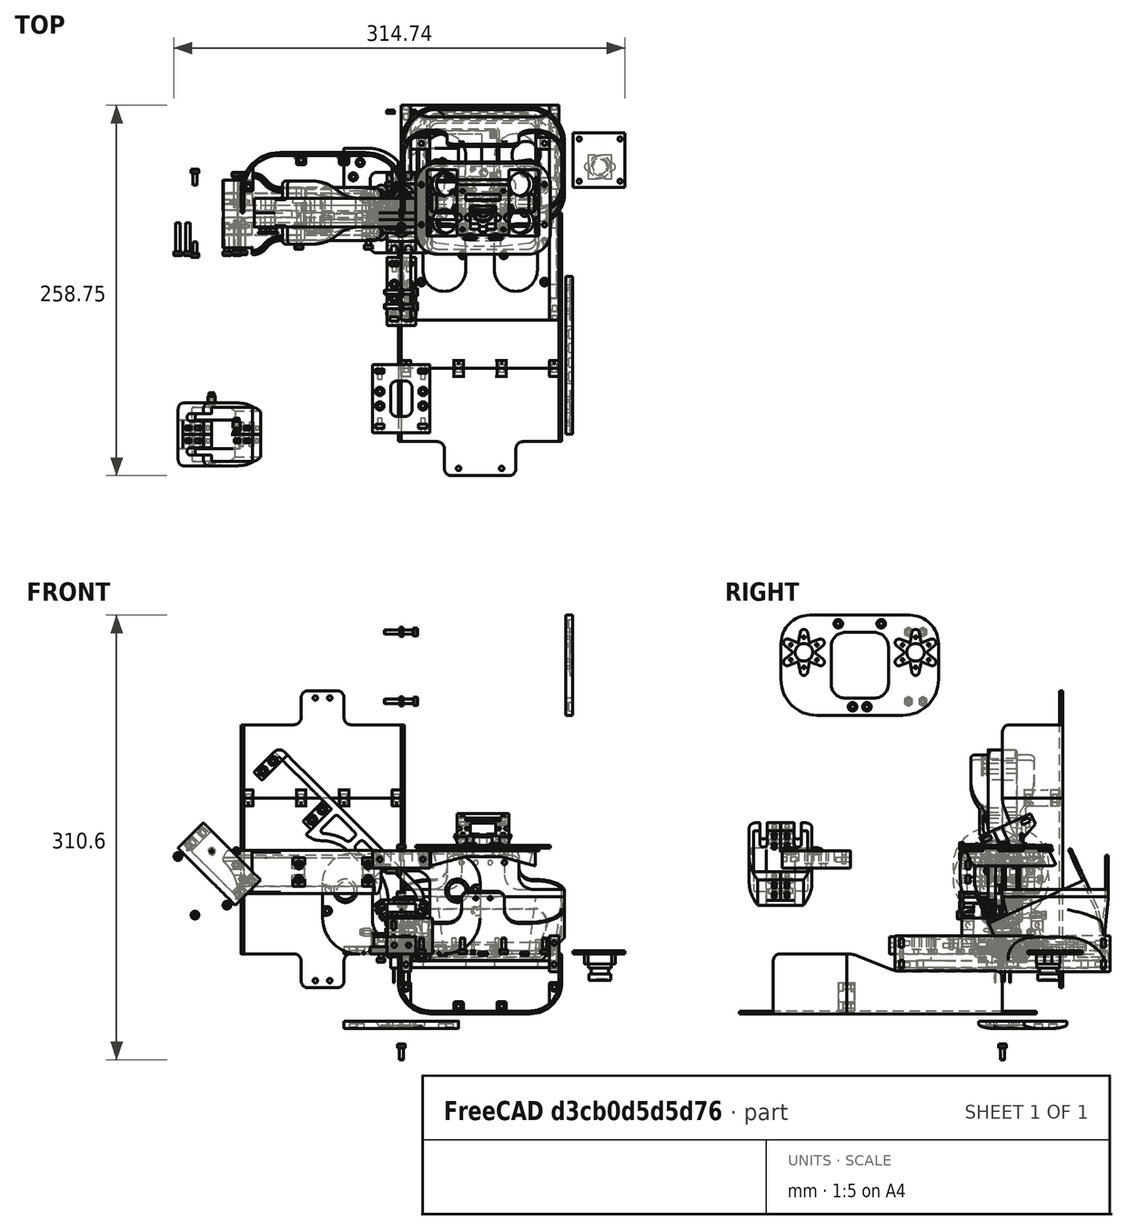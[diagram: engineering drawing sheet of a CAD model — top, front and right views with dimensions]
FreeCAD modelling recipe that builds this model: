
FCSTD DOCUMENT  (FreeCAD 0.18R4 (GitTag))
Label: spotmicroesp32_assembled_quick_and_dirty
License: CreativeCommons Attribution-NonCommercial
LicenseURL: http://creativecommons.org/licenses/by-nc/4.0/
objects: Sketcher::SketchObject×2327, PartDesign::Pad×1069, PartDesign::Pocket×818, PartDesign::Body×716, PartDesign::Chamfer×539, App::Part×291, PartDesign::Fillet×244, PartDesign::Groove×237, PartDesign::Revolution×56, PartDesign::SubtractivePipe×20, Part::Mirroring×14, Part::FeaturePython×8, PartDesign::Thickness×6, PartDesign::PolarPattern×4, PartDesign::Plane×3, PartDesign::AdditiveLoft×1
note: 8263 computed .brp shape members not serialized (recipe doc carries the construction recipe); baked Part::Feature solids carry a one-line shape summary decoded from their .brp

FEATURE [Sketcher::SketchObject] Sketch241
  MapMode = 5
  Support = -> [XY_Plane067]
  sketch-geometry (9):
    g0: ArcOfCircle CenterX=0 CenterY=0 CenterZ=0 NormalX=0 NormalY=0 NormalZ=1 AngleXU=0 Radius=16.5 StartAngle=2.61799 EndAngle=5.75959
    g1: LineSegment StartX=-14.2894 StartY=8.25 StartZ=0 EndX=-1.3577 EndY=30.6484 EndZ=0
    g2: ArcOfCircle CenterX=23.5 CenterY=16.2968 CenterZ=0 NormalX=0 NormalY=0 NormalZ=1 AngleXU=0 Radius=28.7032 StartAngle=1.5708 EndAngle=2.61799
    g3: LineSegment StartX=23.5 StartY=45 StartZ=0 EndX=40 EndY=45 EndZ=0
    g4: LineSegment StartX=40 StartY=45 StartZ=0 EndX=40 EndY=15 EndZ=0
    g5: LineSegment StartX=40 StartY=15 StartZ=0 EndX=28.6962 EndY=15 EndZ=0
    g6: ArcOfCircle CenterX=28.6962 CenterY=13.2968 CenterZ=0 NormalX=0 NormalY=0 NormalZ=1 AngleXU=0 Radius=1.70319 StartAngle=1.5708 EndAngle=2.61799
    g7: LineSegment StartX=27.2211 StartY=14.1484 StartZ=0 EndX=14.2894 EndY=-8.25 EndZ=0
    g8: LineSegment [constr] StartX=-1.3577 StartY=30.6484 StartZ=0 EndX=27.2211 EndY=14.1484 EndZ=0
  constraints (21):
    c: Tangent(g0,g1) = 1.5708
    c: Tangent(g1,g2) = 1.5708
    c: Tangent(g2,g3) = 1.5708
    c: Perpendicular(g3,g4) = 4.71239
    c: Coincident(g4,g5)
    c: Horizontal(g5)
    c: Tangent(g5,g6) = -1.5708
    c: Tangent(g6,g7) = -1.5708
    c: Parallel(g7,g1)
    c: Radius(g0) = 16.5
    c: Horizontal(g3)
    c: DistanceY(g4,g4) = 30
    c: Tangent(g7,g0) = 1.5708
    c: DistanceX(g0,g4) = 40
    c: Coincident(g8,g1)
    c: Coincident(g8,g6)
    c: Perpendicular(g1,g8)
    c: DistanceX(g3,g3) = 16.5
    c: DistanceY(g0,g4) = 15
    c: Angle(g8) = -0.523599
    c: Coincident(g0,g-1)
FEATURE [PartDesign::Pad] Pad074  label="Baseplate001"
  Length = 5
  Length2 = 100
  Profile = -> Sketch241
  Type = 0
FEATURE [Sketcher::SketchObject] Sketch236
  MapMode = 5
  Placement = pos=(40,-9.6e-15,0) rot=(0.57735,0.57735,0.57735;2.0944rad)
  Support = -> [Pad074]
  sketch-geometry (4):
    g0: ArcOfCircle CenterX=35 CenterY=-21 CenterZ=0 NormalX=0 NormalY=0 NormalZ=1 AngleXU=0 Radius=26 StartAngle=1.17601 EndAngle=1.5708
    g1: LineSegment StartX=35 StartY=5 StartZ=0 EndX=35 EndY=6 EndZ=0
    g2: LineSegment StartX=35 StartY=6 StartZ=0 EndX=45 EndY=6 EndZ=0
    g3: LineSegment StartX=45 StartY=6 StartZ=0 EndX=45 EndY=3 EndZ=0
  constraints (13):
    c: Coincident(g1,g0)
    c: Vertical(g1)
    c: Horizontal(g2)
    c: Coincident(g3,g2)
    c: Vertical(g3)
    c: Coincident(g0,g3)
    c: Coincident(g1,g2)
    c: DistanceY(g1,g1) = 1
    c: DistanceY(g3,g3) = 3
    c: DistanceX(g2,g2) = 10
    c: DistanceY(g-1,g0) = 5
    c: DistanceX(g-1,g0) = 45
    c: Perpendicular(g0,g1)
FEATURE [PartDesign::SubtractivePipe] SubtractivePipe001  label="Smooth Surfaces001"
  AuxilleryCurvelinear = true
  AuxillerySpineTangent = false
  BaseFeature = -> Pad074
  Binormal = (0,0,0)
  Mode = 0
  Profile = -> Sketch236
  Spine = -> Pad074 [Edge19,Edge22,Edge24,Edge4,Edge7,Edge10,Edge13]
  SpineTangent = false
  Transformation = 0
  Transition = 0
FEATURE [Sketcher::SketchObject] Sketch243
  MapMode = 5
  Placement = pos=(0,0,5) rot=(0,0,1;0rad)
  Support = -> [SubtractivePipe001]
  sketch-geometry (3):
    g0: Circle [constr] CenterX=0 CenterY=15 CenterZ=0 NormalX=0 NormalY=0 NormalZ=1 AngleXU=0 Radius=35
    g1: Circle CenterX=28.7228 CenterY=35 CenterZ=0 NormalX=0 NormalY=0 NormalZ=1 AngleXU=0 Radius=2.85
    g2: Circle CenterX=33.541 CenterY=25 CenterZ=0 NormalX=0 NormalY=0 NormalZ=1 AngleXU=0 Radius=2.85
  constraints (9):
    c: PointOnObject(g1,g0)
    c: PointOnObject(g2,g0)
    c: Radius(g0) = 35
    c: Equal(g2,g1)
    c: Radius(g1) = 2.85
    c: DistanceY(g2,g1) = 10
    c: DistanceY(g-1,g0) = 15
    c: DistanceY(g0,g2) = 10
    c: DistanceX(g-1,g0) = 0
FEATURE [PartDesign::Fillet] Fillet043  label="Smooth Edges001"
  Base = -> SubtractivePipe001 [Edge21]
  BaseFeature = -> SubtractivePipe001
  Radius = 1.5
FEATURE [PartDesign::Pocket] Pocket125  label="Screwheads Montage001"
  BaseFeature = -> Fillet043
  Length = 3
  Length2 = 100
  Profile = -> Sketch243
  Type = 0
FEATURE [Sketcher::SketchObject] Sketch234
  MapMode = 5
  Placement = pos=(0,0,2) rot=(0,0,1;0rad)
  Support = -> [Pocket125]
  sketch-geometry (3):
    g0: Circle [constr] CenterX=0 CenterY=15 CenterZ=0 NormalX=0 NormalY=0 NormalZ=1 AngleXU=0 Radius=35
    g1: Circle CenterX=28.7228 CenterY=35 CenterZ=0 NormalX=0 NormalY=0 NormalZ=1 AngleXU=0 Radius=1.6
    g2: Circle CenterX=33.541 CenterY=25 CenterZ=0 NormalX=0 NormalY=0 NormalZ=1 AngleXU=0 Radius=1.6
  constraints (9):
    c: Radius(g0) = 35
    c: PointOnObject(g1,g0)
    c: PointOnObject(g2,g0)
    c: Equal(g2,g1)
    c: Radius(g2) = 1.6
    c: DistanceY(g2,g1) = 10
    c: DistanceY(g-1,g0) = 15
    c: DistanceY(g0,g2) = 10
    c: DistanceX(g-1,g0) = 0
FEATURE [PartDesign::Pocket] Pocket124  label="Screwholes Montage001"
  BaseFeature = -> Pocket125
  Length = 3
  Length2 = 100
  Profile = -> Sketch234
  Type = 0
FEATURE [Sketcher::SketchObject] Sketch235
  MapMode = 5
  Placement = pos=(0,0,5) rot=(0,0,1;0rad)
  Support = -> [Fillet043]
  sketch-geometry (33):
    g0: LineSegment [constr] StartX=11.6913 StartY=6.75 StartZ=0 EndX=0 EndY=13.5 EndZ=0
    g1: LineSegment [constr] StartX=0 StartY=13.5 StartZ=0 EndX=-11.6913 EndY=6.75 EndZ=0
    g2: LineSegment [constr] StartX=-11.6913 StartY=6.75 StartZ=0 EndX=-11.6913 EndY=-6.75 EndZ=0
    g3: LineSegment [constr] StartX=-11.6913 StartY=-6.75 StartZ=0 EndX=0 EndY=-13.5 EndZ=0
    g4: LineSegment [constr] StartX=-6e-16 StartY=-13.5 StartZ=0 EndX=11.6913 EndY=-6.75 EndZ=0
    g5: LineSegment [constr] StartX=11.6913 StartY=-6.75 StartZ=0 EndX=11.6913 EndY=6.75 EndZ=0
    g6: Circle [constr] CenterX=0 CenterY=0 CenterZ=0 NormalX=0 NormalY=0 NormalZ=1 AngleXU=0 Radius=13.5
    g7: LineSegment [constr] StartX=7.5 StartY=9e-16 StartZ=0 EndX=3.75 EndY=6.49519 EndZ=0
    g8: LineSegment [constr] StartX=3.75 StartY=6.49519 StartZ=0 EndX=-3.75 EndY=6.49519 EndZ=0
    g9: LineSegment [constr] StartX=-3.75 StartY=6.49519 StartZ=0 EndX=-7.5 EndY=-9e-16 EndZ=0
    g10: LineSegment [constr] StartX=-7.5 StartY=-9e-16 StartZ=0 EndX=-3.75 EndY=-6.49519 EndZ=0
    g11: LineSegment [constr] StartX=-3.75 StartY=-6.49519 StartZ=0 EndX=3.75 EndY=-6.49519 EndZ=0
    g12: LineSegment [constr] StartX=3.75 StartY=-6.49519 StartZ=0 EndX=7.5 EndY=9e-16 EndZ=0
    g13: Circle [constr] CenterX=0 CenterY=0 CenterZ=0 NormalX=0 NormalY=0 NormalZ=1 AngleXU=0 Radius=7.5
    g14: ArcOfCircle CenterX=11.6913 CenterY=-6.75 CenterZ=0 NormalX=0 NormalY=0 NormalZ=1 AngleXU=0 Radius=2.6 StartAngle=4.34694 EndAngle=7.17223
    g15: ArcOfCircle CenterX=-6e-16 CenterY=-13.5 CenterZ=0 NormalX=0 NormalY=0 NormalZ=1 AngleXU=0 Radius=2.6 StartAngle=3.29974 EndAngle=6.12503
    g16: ArcOfCircle CenterX=-11.6913 CenterY=-6.75 CenterZ=0 NormalX=0 NormalY=0 NormalZ=1 AngleXU=0 Radius=2.6 StartAngle=2.25255 EndAngle=5.07784
    g17: ArcOfCircle CenterX=-11.6913 CenterY=6.75 CenterZ=0 NormalX=0 NormalY=0 NormalZ=1 AngleXU=0 Radius=2.6 StartAngle=1.20535 EndAngle=4.03064
    g18: ArcOfCircle CenterX=0 CenterY=13.5 CenterZ=0 NormalX=0 NormalY=0 NormalZ=1 AngleXU=0 Radius=2.6 StartAngle=0.15815 EndAngle=2.98344
    g19: ArcOfCircle CenterX=11.6913 CenterY=6.75 CenterZ=0 NormalX=0 NormalY=0 NormalZ=1 AngleXU=0 Radius=2.6 StartAngle=5.39414 EndAngle=8.21943
    g20: LineSegment StartX=13.3297 StartY=4.73117 StartZ=0 EndX=7.5 EndY=9e-16 EndZ=0
    g21: LineSegment StartX=7.5 StartY=9e-16 StartZ=0 EndX=13.3297 EndY=-4.73117 EndZ=0
    g22: LineSegment StartX=10.7622 StartY=-9.17831 StartZ=0 EndX=3.75 EndY=-6.49519 EndZ=0
    g23: LineSegment StartX=3.75 StartY=-6.49519 StartZ=0 EndX=2.56755 EndY=-13.9095 EndZ=0
    g24: LineSegment StartX=-2.56755 StartY=-13.9095 StartZ=0 EndX=-3.75 EndY=-6.49519 EndZ=0
    g25: LineSegment StartX=-3.75 StartY=-6.49519 StartZ=0 EndX=-10.7622 EndY=-9.17831 EndZ=0
    g26: LineSegment StartX=-13.3297 StartY=-4.73117 StartZ=0 EndX=-7.5 EndY=-9e-16 EndZ=0
    g27: LineSegment StartX=-7.5 StartY=-9e-16 StartZ=0 EndX=-13.3297 EndY=4.73117 EndZ=0
    g28: LineSegment StartX=-10.7622 StartY=9.17831 StartZ=0 EndX=-3.75 EndY=6.49519 EndZ=0
    g29: LineSegment StartX=-3.75 StartY=6.49519 StartZ=0 EndX=-2.56755 EndY=13.9095 EndZ=0
    g30: LineSegment StartX=2.56755 StartY=13.9095 StartZ=0 EndX=3.75 EndY=6.49519 EndZ=0
    g31: LineSegment StartX=3.75 StartY=6.49519 StartZ=0 EndX=10.7622 EndY=9.17831 EndZ=0
    g32: LineSegment [constr] StartX=11.6913 StartY=6.75 StartZ=0 EndX=-11.6913 EndY=-6.75 EndZ=0
  constraints (70):
    c: Coincident(g0,g1)
    c: Coincident(g1,g2)
    c: Coincident(g2,g3)
    c: Coincident(g3,g4)
    c: Coincident(g4,g5)
    c: Coincident(g5,g0)
    c: Equal(g0, g1-g5) x5
    c: PointOnObject(g0,g6)
    c: PointOnObject(g1,g6)
    c: PointOnObject(g2,g6)
    c: PointOnObject(g3,g6)
    c: PointOnObject(g4,g6)
    c: PointOnObject(g5,g6)
    c: Coincident(g6,g-1)
    c: Radius(g6) = 13.5
    c: Coincident(g7,g8)
    c: Coincident(g8,g9)
    c: Coincident(g9,g10)
    c: Coincident(g10,g11)
    c: Coincident(g11,g12)
    c: Coincident(g12,g7)
    c: Equal(g7, g8-g12) x5
    c: PointOnObject(g7,g13)
    c: PointOnObject(g8,g13)
    c: PointOnObject(g9,g13)
    c: PointOnObject(g10,g13)
    c: PointOnObject(g11,g13)
    c: PointOnObject(g12,g13)
    c: Coincident(g13,g-1)
    c: Radius(g13) = 7.5
    c: Coincident(g14,g4)
    c: Coincident(g15,g3)
    c: Coincident(g16,g2)
    c: Coincident(g17,g1)
    c: Coincident(g18,g0)
    c: Coincident(g19,g0)
    c: Coincident(g20,g7)
    c: Coincident(g21,g20)
    c: Coincident(g22,g11)
    c: Coincident(g23,g22)
    c: Coincident(g24,g10)
    c: Coincident(g25,g24)
    c: Coincident(g26,g9)
    c: Coincident(g28,g8)
    c: Coincident(g29,g28)
    c: Coincident(g30,g7)
    c: Coincident(g31,g30)
    c: Tangent(g22,g14) = 1.5708
    c: Tangent(g23,g15) = 1.5708
    c: Tangent(g24,g15) = 1.5708
    c: Tangent(g26,g16) = 1.5708
    c: Tangent(g21,g14) = 1.5708
    c: Tangent(g16,g25) = 1.5708
    c: Tangent(g29,g18) = 1.5708
    c: Tangent(g30,g18) = 1.5708
    c: Tangent(g31,g19) = 1.5708
    c: Tangent(g20,g19) = 1.5708
    c: Tangent(g27,g17) = 1.5708
    c: Tangent(g17,g28) = 1.5708
    c: Coincident(g27,g26)
    c: Equal(g14,g15)
    c: Equal(g15,g16)
    c: Equal(g16,g17)
    c: Equal(g17,g18)
    c: Equal(g18,g19)
    c: Radius(g14) = 2.6
    c: Coincident(g32,g19)
    c: Coincident(g32,g16)
    c: Perpendicular(g32,g7)
    c: PointOnObject(g18,g-2)
FEATURE [PartDesign::Pocket] Pocket123  label="Servohorn003"
  BaseFeature = -> Pocket124
  Length = 2
  Length2 = 100
  Profile = -> Sketch235
  Type = 0
FEATURE [PartDesign::Fillet] Fillet041  label="Smooth Servhohorn Edges001"
  Base = -> Pocket123 [Edge124,Edge122,Edge129,Edge121,Edge136,Edge120]
  BaseFeature = -> Pocket123
  Radius = 1
FEATURE [Sketcher::SketchObject] Sketch242
  MapMode = 5
  Placement = pos=(0,0,3) rot=(0,0,1;0rad)
  Support = -> [Fillet041]
  sketch-geometry (14):
    g0: LineSegment [constr] StartX=0 StartY=10.5 StartZ=0 EndX=-9.09327 EndY=5.25 EndZ=0
    g1: LineSegment [constr] StartX=-9.09327 StartY=5.25 StartZ=0 EndX=-9.09327 EndY=-5.25 EndZ=0
    g2: LineSegment [constr] StartX=-9.09327 StartY=-5.25 StartZ=0 EndX=0 EndY=-10.5 EndZ=0
    g3: LineSegment [constr] StartX=0 StartY=-10.5 StartZ=0 EndX=9.09327 EndY=-5.25 EndZ=0
    g4: LineSegment [constr] StartX=9.09327 StartY=-5.25 StartZ=0 EndX=9.09327 EndY=5.25 EndZ=0
    g5: LineSegment [constr] StartX=9.09327 StartY=5.25 StartZ=0 EndX=0 EndY=10.5 EndZ=0
    g6: Circle [constr] CenterX=0 CenterY=0 CenterZ=0 NormalX=0 NormalY=0 NormalZ=1 AngleXU=0 Radius=10.5
    g7: LineSegment [constr] StartX=0 StartY=10.5 StartZ=0 EndX=0 EndY=-10.5 EndZ=0
    g8: Circle CenterX=0 CenterY=10.5 CenterZ=0 NormalX=0 NormalY=0 NormalZ=1 AngleXU=0 Radius=0.95
    g9: Circle CenterX=9.09327 CenterY=5.25 CenterZ=0 NormalX=0 NormalY=0 NormalZ=1 AngleXU=0 Radius=0.95
    g10: Circle CenterX=9.09327 CenterY=-5.25 CenterZ=0 NormalX=0 NormalY=0 NormalZ=1 AngleXU=0 Radius=0.95
    g11: Circle CenterX=0 CenterY=-10.5 CenterZ=0 NormalX=0 NormalY=0 NormalZ=1 AngleXU=0 Radius=0.95
    g12: Circle CenterX=-9.09327 CenterY=-5.25 CenterZ=0 NormalX=0 NormalY=0 NormalZ=1 AngleXU=0 Radius=0.95
    g13: Circle CenterX=-9.09327 CenterY=5.25 CenterZ=0 NormalX=0 NormalY=0 NormalZ=1 AngleXU=0 Radius=0.95
  constraints (30):
    c: Coincident(g0,g1)
    c: Coincident(g1,g2)
    c: Coincident(g2,g3)
    c: Coincident(g3,g4)
    c: Coincident(g4,g5)
    c: Coincident(g5,g0)
    c: Equal(g0, g1-g5) x5
    c: PointOnObject(g0,g6)
    c: PointOnObject(g1,g6)
    c: PointOnObject(g2,g6)
    c: PointOnObject(g3,g6)
    c: PointOnObject(g4,g6)
    c: PointOnObject(g5,g6)
    c: Coincident(g6,g-1)
    c: Coincident(g7,g0)
    c: Coincident(g7,g2)
    c: Radius(g6) = 10.5
    c: Coincident(g8,g0)
    c: Coincident(g9,g4)
    c: Coincident(g10,g3)
    c: Coincident(g11,g2)
    c: Coincident(g12,g1)
    c: Coincident(g13,g0)
    c: Equal(g13,g12)
    c: Equal(g12,g11)
    c: Equal(g11,g10)
    c: Equal(g10,g9)
    c: Equal(g9,g8)
    c: Radius(g8) = 0.95
    c: PointOnObject(g8,g-2)
FEATURE [PartDesign::Pocket] Pocket126  label="Servohorn Mounting Holes001"
  BaseFeature = -> Fillet041
  Length = 3
  Length2 = 100
  Profile = -> Sketch242
  Type = 0
FEATURE [Sketcher::SketchObject] Sketch239
  MapMode = 5
  Placement = pos=(0,0,3) rot=(0,0,1;0rad)
  Support = -> [Pocket126]
  sketch-geometry (1):
    g0: Circle CenterX=0 CenterY=0 CenterZ=0 NormalX=0 NormalY=0 NormalZ=1 AngleXU=0 Radius=6.15
  constraints (2):
    c: Coincident(g0,g-1)
    c: Radius(g0) = 6.15
FEATURE [PartDesign::Pocket] Pocket122  label="Servohorn Axis001"
  BaseFeature = -> Pocket126
  Length = 3
  Length2 = 100
  Profile = -> Sketch239
  Type = 0
FEATURE [PartDesign::Fillet] Fillet042  label="Smooth End Egde001"
  Base = -> Pocket122 [Edge150]
  BaseFeature = -> Pocket122
  Radius = 0.4
FEATURE [PartDesign::Body] Body041  label="Limb_Servohorn_Mount_long_v005"
  Group = -> [Sketch241,Pad074,Sketch236,SubtractivePipe001,Fillet043,Sketch243,Pocket125,Sketch234,Pocket124,Sketch235,Pocket123,Fillet041,Sketch242,Pocket126,Sketch239,Pocket122,Fillet042]
  Origin = -> Origin071
  Tip = -> Fillet042
FEATURE [Sketcher::SketchObject] Sketch244
  MapMode = 5
  Support = -> [XY_Plane063]
  sketch-geometry (64):
    g0: LineSegment [constr] StartX=-3.75 StartY=6.49519 StartZ=0 EndX=-7.5 EndY=0 EndZ=0
    g1: LineSegment [constr] StartX=-7.5 StartY=0 StartZ=0 EndX=-3.75 EndY=-6.49519 EndZ=0
    g2: LineSegment [constr] StartX=-3.75 StartY=-6.49519 StartZ=0 EndX=3.75 EndY=-6.49519 EndZ=0
    g3: LineSegment [constr] StartX=3.75 StartY=-6.49519 StartZ=0 EndX=7.5 EndY=0 EndZ=0
    g4: LineSegment [constr] StartX=7.5 StartY=0 StartZ=0 EndX=3.75 EndY=6.49519 EndZ=0
    g5: LineSegment [constr] StartX=3.75 StartY=6.49519 StartZ=0 EndX=-3.75 EndY=6.49519 EndZ=0
    g6: Circle [constr] CenterX=0 CenterY=0 CenterZ=0 NormalX=0 NormalY=0 NormalZ=1 AngleXU=0 Radius=7.5
    g7: LineSegment [constr] StartX=0 StartY=7.5 StartZ=0 EndX=-6.49519 EndY=3.75 EndZ=0
    g8: LineSegment [constr] StartX=-6.49519 StartY=3.75 StartZ=0 EndX=-6.49519 EndY=-3.75 EndZ=0
    g9: LineSegment [constr] StartX=-6.49519 StartY=-3.75 StartZ=0 EndX=9.8e-15 EndY=-7.5 EndZ=0
    g10: LineSegment [constr] StartX=9.8e-15 StartY=-7.5 StartZ=0 EndX=6.49519 EndY=-3.75 EndZ=0
    g11: LineSegment [constr] StartX=6.49519 StartY=-3.75 StartZ=0 EndX=6.49519 EndY=3.75 EndZ=0
    g12: LineSegment [constr] StartX=6.49519 StartY=3.75 StartZ=0 EndX=0 EndY=7.5 EndZ=0
    g13: Circle [constr] CenterX=0 CenterY=0 CenterZ=0 NormalX=0 NormalY=0 NormalZ=1 AngleXU=0 Radius=7.5
    g14: LineSegment [constr] StartX=0 StartY=10.5 StartZ=0 EndX=-9.09327 EndY=5.25 EndZ=0
    g15: LineSegment [constr] StartX=-9.09327 StartY=5.25 StartZ=0 EndX=-9.09327 EndY=-5.25 EndZ=0
    g16: LineSegment [constr] StartX=-9.09327 StartY=-5.25 StartZ=0 EndX=-1.42e-14 EndY=-10.5 EndZ=0
    g17: LineSegment [constr] StartX=-1.42e-14 StartY=-10.5 StartZ=0 EndX=9.09327 EndY=-5.25 EndZ=0
    g18: LineSegment [constr] StartX=9.09327 StartY=-5.25 StartZ=0 EndX=9.09327 EndY=5.25 EndZ=0
    g19: LineSegment [constr] StartX=9.09327 StartY=5.25 StartZ=0 EndX=0 EndY=10.5 EndZ=0
    g20: Circle [constr] CenterX=0 CenterY=0 CenterZ=0 NormalX=0 NormalY=0 NormalZ=1 AngleXU=0 Radius=10.5
    g21: LineSegment [constr] StartX=0 StartY=13.5 StartZ=0 EndX=-11.6913 EndY=6.75 EndZ=0
    g22: LineSegment [constr] StartX=-11.6913 StartY=6.75 StartZ=0 EndX=-11.6913 EndY=-6.75 EndZ=0
    g23: LineSegment [constr] StartX=-11.6913 StartY=-6.75 StartZ=0 EndX=0 EndY=-13.5 EndZ=0
    g24: LineSegment [constr] StartX=0 StartY=-13.5 StartZ=0 EndX=11.6913 EndY=-6.75 EndZ=0
    g25: LineSegment [constr] StartX=11.6913 StartY=-6.75 StartZ=0 EndX=11.6913 EndY=6.75 EndZ=0
    g26: LineSegment [constr] StartX=11.6913 StartY=6.75 StartZ=0 EndX=0 EndY=13.5 EndZ=0
    g27: Circle [constr] CenterX=0 CenterY=0 CenterZ=0 NormalX=0 NormalY=0 NormalZ=1 AngleXU=0 Radius=13.5
    g28: ArcOfCircle CenterX=0 CenterY=13.5 CenterZ=0 NormalX=0 NormalY=0 NormalZ=1 AngleXU=0 Radius=2.5 StartAngle=0.171439 EndAngle=2.97015
    g29: ArcOfCircle CenterX=11.6913 CenterY=6.75 CenterZ=0 NormalX=0 NormalY=0 NormalZ=1 AngleXU=0 Radius=2.5 StartAngle=5.40743 EndAngle=8.20614
    g30: ArcOfCircle CenterX=11.6913 CenterY=-6.75 CenterZ=0 NormalX=0 NormalY=0 NormalZ=1 AngleXU=0 Radius=2.5 StartAngle=4.36023 EndAngle=7.15894
    g31: ArcOfCircle CenterX=0 CenterY=-13.5 CenterZ=0 NormalX=0 NormalY=0 NormalZ=1 AngleXU=0 Radius=2.5 StartAngle=3.31303 EndAngle=6.11175
    g32: ArcOfCircle CenterX=-11.6913 CenterY=-6.75 CenterZ=0 NormalX=0 NormalY=0 NormalZ=1 AngleXU=0 Radius=2.5 StartAngle=2.26583 EndAngle=5.06455
    g33: ArcOfCircle CenterX=-11.6913 CenterY=6.75 CenterZ=0 NormalX=0 NormalY=0 NormalZ=1 AngleXU=0 Radius=2.5 StartAngle=1.21864 EndAngle=4.01735
    g34: LineSegment StartX=-10.829 StartY=9.09658 StartZ=0 EndX=-3.75 EndY=6.49519 EndZ=0
    g35: LineSegment StartX=-3.75 StartY=6.49519 StartZ=0 EndX=-2.46335 EndY=13.9265 EndZ=0
    g36: LineSegment StartX=2.46335 StartY=13.9265 StartZ=0 EndX=3.75 EndY=6.49519 EndZ=0
    g37: LineSegment StartX=3.75 StartY=6.49519 StartZ=0 EndX=10.829 EndY=9.09658 EndZ=0
    g38: LineSegment StartX=13.2924 StartY=4.82993 StartZ=0 EndX=7.5 EndY=0 EndZ=0
    g39: LineSegment StartX=7.5 StartY=0 StartZ=0 EndX=13.2924 EndY=-4.82993 EndZ=0
    g40: LineSegment StartX=10.829 StartY=-9.09658 StartZ=0 EndX=3.75 EndY=-6.49519 EndZ=0
    g41: LineSegment StartX=3.75 StartY=-6.49519 StartZ=0 EndX=2.46335 EndY=-13.9265 EndZ=0
    g42: LineSegment StartX=-2.46335 StartY=-13.9265 StartZ=0 EndX=-3.75 EndY=-6.49519 EndZ=0
    g43: LineSegment StartX=-3.75 StartY=-6.49519 StartZ=0 EndX=-10.829 EndY=-9.09658 EndZ=0
    g44: LineSegment StartX=-13.2924 StartY=-4.82993 StartZ=0 EndX=-7.5 EndY=0 EndZ=0
    g45: LineSegment StartX=-7.5 StartY=0 StartZ=0 EndX=-13.2924 EndY=4.82993 EndZ=0
    g46: Circle CenterX=-11.6913 CenterY=6.75 CenterZ=0 NormalX=0 NormalY=0 NormalZ=1 AngleXU=0 Radius=0.75
    g47: Circle CenterX=-9.09327 CenterY=5.25 CenterZ=0 NormalX=0 NormalY=0 NormalZ=1 AngleXU=0 Radius=0.75
    g48: Circle CenterX=-6.49519 CenterY=3.75 CenterZ=0 NormalX=0 NormalY=0 NormalZ=1 AngleXU=0 Radius=0.75
    g49: Circle CenterX=0 CenterY=13.5 CenterZ=0 NormalX=0 NormalY=0 NormalZ=1 AngleXU=0 Radius=0.75
    g50: Circle CenterX=0 CenterY=10.5 CenterZ=0 NormalX=0 NormalY=0 NormalZ=1 AngleXU=0 Radius=0.75
    g51: Circle CenterX=0 CenterY=7.5 CenterZ=0 NormalX=0 NormalY=0 NormalZ=1 AngleXU=0 Radius=0.75
    g52: Circle CenterX=11.6913 CenterY=6.75 CenterZ=0 NormalX=0 NormalY=0 NormalZ=1 AngleXU=0 Radius=0.75
    g53: Circle CenterX=9.09327 CenterY=5.25 CenterZ=0 NormalX=0 NormalY=0 NormalZ=1 AngleXU=0 Radius=0.75
    g54: Circle CenterX=6.49519 CenterY=3.75 CenterZ=0 NormalX=0 NormalY=0 NormalZ=1 AngleXU=0 Radius=0.75
    g55: Circle CenterX=11.6913 CenterY=-6.75 CenterZ=0 NormalX=0 NormalY=0 NormalZ=1 AngleXU=0 Radius=0.75
    g56: Circle CenterX=9.09327 CenterY=-5.25 CenterZ=0 NormalX=0 NormalY=0 NormalZ=1 AngleXU=0 Radius=0.75
    g57: Circle CenterX=6.49519 CenterY=-3.75 CenterZ=0 NormalX=0 NormalY=0 NormalZ=1 AngleXU=0 Radius=0.75
    g58: Circle CenterX=9.8e-15 CenterY=-7.5 CenterZ=0 NormalX=0 NormalY=0 NormalZ=1 AngleXU=0 Radius=0.75
    g59: Circle CenterX=-1.42e-14 CenterY=-10.5 CenterZ=0 NormalX=0 NormalY=0 NormalZ=1 AngleXU=0 Radius=0.75
    g60: Circle CenterX=0 CenterY=-13.5 CenterZ=0 NormalX=0 NormalY=0 NormalZ=1 AngleXU=0 Radius=0.75
    g61: Circle CenterX=-11.6913 CenterY=-6.75 CenterZ=0 NormalX=0 NormalY=0 NormalZ=1 AngleXU=0 Radius=0.75
    g62: Circle CenterX=-9.09327 CenterY=-5.25 CenterZ=0 NormalX=0 NormalY=0 NormalZ=1 AngleXU=0 Radius=0.75
    g63: Circle CenterX=-6.49519 CenterY=-3.75 CenterZ=0 NormalX=0 NormalY=0 NormalZ=1 AngleXU=0 Radius=0.75
  constraints (136):
    c: Coincident(g0,g1)
    c: Coincident(g1,g2)
    c: Coincident(g2,g3)
    c: Coincident(g3,g4)
    c: Coincident(g4,g5)
    c: Coincident(g5,g0)
    c: Equal(g0, g1-g5) x5
    c: PointOnObject(g0,g6)
    c: PointOnObject(g1,g6)
    c: PointOnObject(g2,g6)
    c: PointOnObject(g3,g6)
    c: PointOnObject(g4,g6)
    c: PointOnObject(g5,g6)
    c: Coincident(g6,g-1)
    c: Coincident(g7,g8)
    c: Coincident(g8,g9)
    c: Coincident(g9,g10)
    c: Coincident(g10,g11)
    c: Coincident(g11,g12)
    c: Coincident(g12,g7)
    c: Equal(g7, g8-g12) x5
    c: PointOnObject(g7,g13)
    c: PointOnObject(g8,g13)
    c: PointOnObject(g9,g13)
    c: PointOnObject(g10,g13)
    c: PointOnObject(g11,g13)
    c: PointOnObject(g12,g13)
    c: Coincident(g13,g-1)
    c: PointOnObject(g12,g6)
    c: PointOnObject(g7,g-2)
    c: Horizontal(g5)
    c: Radius(g6) = 7.5
    c: Coincident(g14,g15)
    c: Coincident(g15,g16)
    c: Coincident(g16,g17)
    c: Coincident(g17,g18)
    c: Coincident(g18,g19)
    c: Coincident(g19,g14)
    c: Equal(g14, g15-g19) x5
    c: PointOnObject(g14,g20)
    c: PointOnObject(g15,g20)
    c: PointOnObject(g16,g20)
    c: PointOnObject(g17,g20)
    c: PointOnObject(g18,g20)
    c: PointOnObject(g19,g20)
    c: Coincident(g20,g-1)
    c: PointOnObject(g19,g-2)
    c: Radius(g20) = 10.5
    c: Coincident(g21,g22)
    c: Coincident(g22,g23)
    c: Coincident(g23,g24)
    c: Coincident(g24,g25)
    c: Coincident(g25,g26)
    c: Coincident(g26,g21)
    c: Equal(g21, g22-g26) x5
    c: PointOnObject(g21,g27)
    c: PointOnObject(g22,g27)
    c: PointOnObject(g23,g27)
    c: PointOnObject(g24,g27)
    c: PointOnObject(g25,g27)
    c: PointOnObject(g26,g27)
    c: Coincident(g27,g-1)
    c: PointOnObject(g26,g-2)
    c: Radius(g27) = 13.5
    c: Coincident(g28,g21)
    c: Coincident(g29,g25)
    c: Coincident(g30,g24)
    c: Coincident(g31,g23)
    c: Coincident(g32,g22)
    c: Coincident(g33,g21)
    c: Coincident(g34,g0)
    c: Coincident(g35,g34)
    c: Coincident(g36,g4)
    c: Coincident(g37,g36)
    c: Coincident(g38,g3)
    c: Coincident(g39,g38)
    c: Coincident(g40,g2)
    c: Coincident(g41,g40)
    c: Coincident(g42,g1)
    c: Coincident(g43,g42)
    c: Coincident(g44,g0)
    c: Coincident(g45,g44)
    c: Tangent(g35,g28) = 1.5708
    c: Tangent(g36,g28) = 1.5708
    c: Tangent(g37,g29) = 1.5708
    c: Tangent(g38,g29) = 1.5708
    c: Tangent(g39,g30) = 1.5708
    c: Tangent(g40,g30) = 1.5708
    c: Tangent(g41,g31) = 1.5708
    c: Tangent(g42,g31) = 1.5708
    c: Tangent(g43,g32) = 1.5708
    c: Tangent(g44,g32) = 1.5708
    c: Tangent(g45,g33) = 1.5708
    c: Tangent(g34,g33) = 1.5708
    c: Radius(g29) = 2.5
    c: Equal(g29,g28)
    c: Equal(g28,g33)
    c: Equal(g33,g32)
    c: Equal(g32,g31)
    c: Equal(g31,g30)
    c: Coincident(g46,g33)
    c: Coincident(g47,g14)
    c: Coincident(g48,g7)
    c: Coincident(g49,g28)
    c: Coincident(g50,g14)
    c: Coincident(g51,g7)
    c: Coincident(g52,g29)
    c: Coincident(g53,g18)
    c: Coincident(g54,g11)
    c: Coincident(g55,g30)
    c: Coincident(g56,g17)
    c: Coincident(g57,g10)
    c: Coincident(g58,g9)
    c: Coincident(g59,g16)
    c: Coincident(g60,g31)
    c: Coincident(g61,g32)
    c: Coincident(g62,g15)
    c: Coincident(g63,g8)
    c: Equal(g61,g62)
    c: Equal(g62,g63)
    c: Equal(g63,g58)
    c: Equal(g58,g59)
    c: Equal(g59,g60)
    c: Equal(g60,g55)
    c: Equal(g55,g56)
    c: Equal(g56,g57)
    c: Equal(g57,g54)
    c: Equal(g54,g53)
    c: Equal(g53,g52)
    c: Equal(g52,g51)
    c: Equal(g51,g50)
    c: Equal(g50,g49)
    c: Equal(g49,g46)
    c: Equal(g46,g47)
    c: Equal(g47,g48)
    c: Radius(g55) = 0.75
FEATURE [PartDesign::Pad] Pad075
  Length = 2
  Length2 = 100
  Profile = -> Sketch244
  Type = 0
FEATURE [Sketcher::SketchObject] Sketch237
  MapMode = 5
  Placement = pos=(0,0,2) rot=(0,0,1;0rad)
  Support = -> [Pad075]
  sketch-geometry (2):
    g0: Circle CenterX=0 CenterY=0 CenterZ=0 NormalX=0 NormalY=0 NormalZ=1 AngleXU=0 Radius=5
    g1: Circle CenterX=0 CenterY=0 CenterZ=0 NormalX=0 NormalY=0 NormalZ=1 AngleXU=0 Radius=3.5
  constraints (4):
    c: Coincident(g0,g-1)
    c: Coincident(g1,g0)
    c: Radius(g1) = 3.5
    c: Radius(g0) = 5
FEATURE [PartDesign::Pocket] Pocket121
  BaseFeature = -> Pad075
  Length = 1
  Length2 = 100
  Profile = -> Sketch237
  Type = 0
FEATURE [Sketcher::SketchObject] Sketch238
  MapMode = 5
  Placement = pos=(0,0,2) rot=(0,0,1;0rad)
  Support = -> [Pocket121]
  sketch-geometry (1):
    g0: Circle CenterX=0 CenterY=0 CenterZ=0 NormalX=0 NormalY=0 NormalZ=1 AngleXU=0 Radius=3
  constraints (2):
    c: Coincident(g0,g-1)
    c: Radius(g0) = 3
FEATURE [PartDesign::Pocket] Pocket127
  BaseFeature = -> Pocket121
  Length = 1
  Length2 = 100
  Profile = -> Sketch238
  Type = 0
FEATURE [Sketcher::SketchObject] Sketch240
  MapMode = 5
  Placement = pos=(0,0,1) rot=(0,0,1;0rad)
  Support = -> [Pocket127]
  sketch-geometry (1):
    g0: Circle CenterX=0 CenterY=0 CenterZ=0 NormalX=0 NormalY=0 NormalZ=1 AngleXU=0 Radius=1.5
  constraints (2):
    c: Coincident(g0,g-1)
    c: Radius(g0) = 1.5
FEATURE [PartDesign::Pocket] Pocket130
  BaseFeature = -> Pocket127
  Length = 5
  Length2 = 100
  Profile = -> Sketch240
  Type = 0
FEATURE [Sketcher::SketchObject] Sketch245
  MapMode = 5
  Placement = pos=(0,0,0) rot=(1,0,0;3.14159rad)
  Support = -> [Pocket130]
  sketch-geometry (2):
    g0: Circle CenterX=0 CenterY=0 CenterZ=0 NormalX=0 NormalY=0 NormalZ=1 AngleXU=0 Radius=4.5
    g1: Circle CenterX=0 CenterY=0 CenterZ=0 NormalX=0 NormalY=0 NormalZ=1 AngleXU=0 Radius=3
  constraints (4):
    c: Coincident(g0,g-1)
    c: Coincident(g1,g0)
    c: Radius(g0) = 4.5
    c: Radius(g1) = 3
FEATURE [PartDesign::Pad] Pad073
  BaseFeature = -> Pocket130
  Length = 3
  Length2 = 100
  Profile = -> Sketch245
  Type = 0
FEATURE [PartDesign::Fillet] Fillet044
  Base = -> Pad073 [Face5,Edge96,Face4]
  BaseFeature = -> Pad073
  Radius = 0.2
FEATURE [PartDesign::Body] Body042  label="Futuba FSH6B001"
  Group = -> [Sketch244,Pad075,Sketch237,Pocket121,Sketch238,Pocket127,Sketch240,Pocket130,Sketch245,Pad073,Fillet044]
  Origin = -> Origin075
  Tip = -> Fillet044
FEATURE [App::Part] Part013  label="Servohorn002"
  Group = -> [Body042]
  Origin = -> Origin072
  Placement = pos=(0,0,3) rot=(0,0,1;0rad)
FEATURE [Sketcher::SketchObject] Sketch247
  MapMode = 5
  Support = -> [XY_Plane079]
FEATURE [Sketcher::SketchObject] Sketch249
  MapMode = 5
  Support = -> [XY_Plane078]
  sketch-geometry (1):
    g0: Circle CenterX=0 CenterY=0 CenterZ=0 NormalX=0 NormalY=0 NormalZ=1 AngleXU=0 Radius=1.9
  constraints (2):
    c: Coincident(g0,g-1)
    c: Radius(g0) = 1.9
FEATURE [PartDesign::Pad] Pad078  label="M3x8 Head007"
  Length = 2
  Length2 = 100
  Profile = -> Sketch249
  Type = 0
FEATURE [Sketcher::SketchObject] Sketch250
  MapMode = 5
  Placement = pos=(0,0,2) rot=(0,0,1;0rad)
  Support = -> [Pad078]
  sketch-geometry (1):
    g0: Circle CenterX=0 CenterY=0 CenterZ=0 NormalX=0 NormalY=0 NormalZ=1 AngleXU=0 Radius=1
  constraints (2):
    c: Coincident(g0,g-1)
    c: Radius(g0) = 1
FEATURE [PartDesign::Pad] Pad079  label="M3x8 Thread007"
  BaseFeature = -> Pad078
  Length = 8
  Length2 = 100
  Profile = -> Sketch250
  Type = 0
FEATURE [Sketcher::SketchObject] Sketch246
  MapMode = 5
  Placement = pos=(0,0,0) rot=(1,0,0;3.14159rad)
  Support = -> [Pad079]
  sketch-geometry (7):
    g0: LineSegment StartX=0.77 StartY=0.44456 StartZ=0 EndX=0 EndY=0.889119 EndZ=0
    g1: LineSegment StartX=0 StartY=0.889119 StartZ=0 EndX=-0.77 EndY=0.44456 EndZ=0
    g2: LineSegment StartX=-0.77 StartY=0.44456 StartZ=0 EndX=-0.77 EndY=-0.44456 EndZ=0
    g3: LineSegment StartX=-0.77 StartY=-0.44456 StartZ=0 EndX=3.85628e-11 EndY=-0.889119 EndZ=0
    g4: LineSegment StartX=3.85628e-11 StartY=-0.889119 StartZ=0 EndX=0.77 EndY=-0.44456 EndZ=0
    g5: LineSegment StartX=0.77 StartY=-0.44456 StartZ=0 EndX=0.77 EndY=0.44456 EndZ=0
    g6: Circle [constr] CenterX=0 CenterY=0 CenterZ=0 NormalX=0 NormalY=0 NormalZ=1 AngleXU=0 Radius=0.889119
  constraints (16):
    c: Coincident(g0,g1)
    c: Coincident(g1,g2)
    c: Coincident(g2,g3)
    c: Coincident(g3,g4)
    c: Coincident(g4,g5)
    c: Coincident(g5,g0)
    c: Equal(g0, g1-g5) x5
    c: PointOnObject(g0,g6)
    c: PointOnObject(g1,g6)
    c: PointOnObject(g2,g6)
    c: PointOnObject(g3,g6)
    c: PointOnObject(g4,g6)
    c: PointOnObject(g5,g6)
    c: Coincident(g6,g-1)
    c: PointOnObject(g0,g-2)
    c: DistanceX(g1,g0) = 1.54
FEATURE [PartDesign::Pocket] Pocket129  label="M3x8 Wrench008"
  BaseFeature = -> Pad079
  Length = 1
  Length2 = 100
  Profile = -> Sketch246
  Type = 0
FEATURE [PartDesign::Chamfer] Chamfer025  label="M3x8 Smooth012"
  Base = -> Pocket129 [Face11,Edge2,Edge24,Edge3]
  BaseFeature = -> Pocket129
  Size = 0.2
FEATURE [Sketcher::SketchObject] Sketch251
  MapMode = 5
  Support = -> [XY_Plane079]
FEATURE [Sketcher::SketchObject] Sketch252
  MapMode = 5
  Support = -> [XY_Plane079]
  sketch-geometry (8):
    g0: LineSegment StartX=0 StartY=2.3094 StartZ=0 EndX=-2 EndY=1.1547 EndZ=0
    g1: LineSegment StartX=-2 StartY=1.1547 StartZ=0 EndX=-2 EndY=-1.1547 EndZ=0
    g2: LineSegment StartX=-2 StartY=-1.1547 StartZ=0 EndX=-2e-16 EndY=-2.3094 EndZ=0
    g3: LineSegment StartX=-2e-16 StartY=-2.3094 StartZ=0 EndX=2 EndY=-1.1547 EndZ=0
    g4: LineSegment StartX=2 StartY=-1.1547 StartZ=0 EndX=2 EndY=1.1547 EndZ=0
    g5: LineSegment StartX=2 StartY=1.1547 StartZ=0 EndX=0 EndY=2.3094 EndZ=0
    g6: Circle [constr] CenterX=0 CenterY=0 CenterZ=0 NormalX=0 NormalY=0 NormalZ=1 AngleXU=0 Radius=2.3094
    g7: Circle CenterX=0 CenterY=0 CenterZ=0 NormalX=0 NormalY=0 NormalZ=1 AngleXU=0 Radius=1
  constraints (18):
    c: Coincident(g0,g1)
    c: Coincident(g1,g2)
    c: Coincident(g2,g3)
    c: Coincident(g3,g4)
    c: Coincident(g4,g5)
    c: Coincident(g5,g0)
    c: Equal(g0, g1-g5) x5
    c: PointOnObject(g0,g6)
    c: PointOnObject(g1,g6)
    c: PointOnObject(g2,g6)
    c: PointOnObject(g3,g6)
    c: PointOnObject(g4,g6)
    c: PointOnObject(g5,g6)
    c: Coincident(g6,g-1)
    c: PointOnObject(g5,g-2)
    c: DistanceX(g0,g4) = 4
    c: Coincident(g7,g-1)
    c: Radius(g7) = 1
FEATURE [PartDesign::Pad] Pad077  label="M3 Nut Primitive008"
  Length = 0.6
  Length2 = 0.6
  Profile = -> Sketch252
  Type = 4
FEATURE [Sketcher::SketchObject] Sketch248
  ExternalGeometry = -> [Pad077]
  MapMode = 5
  Placement = pos=(0,0,0) rot=(0.57735,0.57735,0.57735;2.0944rad)
  Support = -> [YZ_Plane078]
  sketch-geometry (6):
    g0: LineSegment StartX=-1.9594 StartY=0.6 StartZ=0 EndX=-2.8094 EndY=0.6 EndZ=0
    g1: LineSegment StartX=-2.8094 StartY=0.6 StartZ=0 EndX=-2.8094 EndY=-0.6 EndZ=0
    g2: LineSegment StartX=-2.8094 StartY=-0.6 StartZ=0 EndX=-1.9594 EndY=-0.6 EndZ=0
    g3: LineSegment StartX=-1.9594 StartY=-0.6 StartZ=0 EndX=-2.3094 EndY=-0.4 EndZ=0
    g4: LineSegment StartX=-2.3094 StartY=-0.4 StartZ=0 EndX=-2.3094 EndY=0.4 EndZ=0
    g5: LineSegment StartX=-2.3094 StartY=0.4 StartZ=0 EndX=-1.9594 EndY=0.6 EndZ=0
  constraints (15):
    c: Horizontal(g0)
    c: Coincident(g0,g1)
    c: Coincident(g1,g2)
    c: Coincident(g2,g3)
    c: Coincident(g3,g4)
    c: Coincident(g4,g5)
    c: Coincident(g5,g0)
    c: Symmetric(g4,g3,g-1)
    c: Symmetric(g0,g2,g-1)
    c: Symmetric(g1,g0,g-1)
    c: DistanceX(g0,g4) = 0.5
    c: DistanceY(g3,g4) = 0.8
    c: DistanceY(g1,g0) = 1.2
    c: PointOnObject(g3,g-3)
    c: DistanceX(g4,g0) = 0.35
FEATURE [PartDesign::Groove] Groove007  label="M3 Nut Smooth007"
  Angle = 360
  Axis = (-2e-16,3e-16,1)
  Base = (0,0,0)
  BaseFeature = -> Pad077
  Profile = -> Sketch248
  ReferenceAxis = -> Sketch248 [V_Axis]
  Reversed = true
FEATURE [PartDesign::Chamfer] Chamfer022  label="M3 Nut Smooth Hole010"
  Base = -> Groove007 [Edge24,Edge23]
  BaseFeature = -> Groove007
  Size = 0.2
FEATURE [Sketcher::SketchObject] Sketch253
  MapMode = 5
  Support = -> [XY_Plane058]
FEATURE [Sketcher::SketchObject] Sketch256
  MapMode = 5
  Support = -> [XY_Plane060]
  sketch-geometry (8):
    g0: LineSegment StartX=0 StartY=2.3094 StartZ=0 EndX=-2 EndY=1.1547 EndZ=0
    g1: LineSegment StartX=-2 StartY=1.1547 StartZ=0 EndX=-2 EndY=-1.1547 EndZ=0
    g2: LineSegment StartX=-2 StartY=-1.1547 StartZ=0 EndX=-2e-16 EndY=-2.3094 EndZ=0
    g3: LineSegment StartX=-2e-16 StartY=-2.3094 StartZ=0 EndX=2 EndY=-1.1547 EndZ=0
    g4: LineSegment StartX=2 StartY=-1.1547 StartZ=0 EndX=2 EndY=1.1547 EndZ=0
    g5: LineSegment StartX=2 StartY=1.1547 StartZ=0 EndX=0 EndY=2.3094 EndZ=0
    g6: Circle [constr] CenterX=0 CenterY=0 CenterZ=0 NormalX=0 NormalY=0 NormalZ=1 AngleXU=0 Radius=2.3094
    g7: Circle CenterX=0 CenterY=0 CenterZ=0 NormalX=0 NormalY=0 NormalZ=1 AngleXU=0 Radius=1
  constraints (18):
    c: Coincident(g0,g1)
    c: Coincident(g1,g2)
    c: Coincident(g2,g3)
    c: Coincident(g3,g4)
    c: Coincident(g4,g5)
    c: Coincident(g5,g0)
    c: Equal(g0, g1-g5) x5
    c: PointOnObject(g0,g6)
    c: PointOnObject(g1,g6)
    c: PointOnObject(g2,g6)
    c: PointOnObject(g3,g6)
    c: PointOnObject(g4,g6)
    c: PointOnObject(g5,g6)
    c: Coincident(g6,g-1)
    c: PointOnObject(g5,g-2)
    c: DistanceX(g0,g4) = 4
    c: Coincident(g7,g-1)
    c: Radius(g7) = 1
FEATURE [PartDesign::Pad] Pad086  label="M3 Nut Primitive010"
  Length = 0.6
  Length2 = 0.6
  Profile = -> Sketch256
  Type = 4
FEATURE [Sketcher::SketchObject] Sketch254
  ExternalGeometry = -> [Pad086]
  MapMode = 5
  Placement = pos=(0,0,0) rot=(0.57735,0.57735,0.57735;2.0944rad)
  Support = -> [YZ_Plane058]
  sketch-geometry (6):
    g0: LineSegment StartX=-1.9594 StartY=0.6 StartZ=0 EndX=-2.8094 EndY=0.6 EndZ=0
    g1: LineSegment StartX=-2.8094 StartY=0.6 StartZ=0 EndX=-2.8094 EndY=-0.6 EndZ=0
    g2: LineSegment StartX=-2.8094 StartY=-0.6 StartZ=0 EndX=-1.9594 EndY=-0.6 EndZ=0
    g3: LineSegment StartX=-1.9594 StartY=-0.6 StartZ=0 EndX=-2.3094 EndY=-0.4 EndZ=0
    g4: LineSegment StartX=-2.3094 StartY=-0.4 StartZ=0 EndX=-2.3094 EndY=0.4 EndZ=0
    g5: LineSegment StartX=-2.3094 StartY=0.4 StartZ=0 EndX=-1.9594 EndY=0.6 EndZ=0
  constraints (15):
    c: Horizontal(g0)
    c: Coincident(g0,g1)
    c: Coincident(g1,g2)
    c: Coincident(g2,g3)
    c: Coincident(g3,g4)
    c: Coincident(g4,g5)
    c: Coincident(g5,g0)
    c: Symmetric(g4,g3,g-1)
    c: Symmetric(g0,g2,g-1)
    c: Symmetric(g1,g0,g-1)
    c: DistanceX(g0,g4) = 0.5
    c: DistanceY(g3,g4) = 0.8
    c: DistanceY(g1,g0) = 1.2
    c: PointOnObject(g3,g-3)
    c: DistanceX(g4,g0) = 0.35
FEATURE [PartDesign::Groove] Groove009  label="M3 Nut Smooth009"
  Angle = 360
  Axis = (-2e-16,3e-16,1)
  Base = (0,0,0)
  BaseFeature = -> Pad086
  Profile = -> Sketch254
  ReferenceAxis = -> Sketch254 [V_Axis]
  Reversed = true
FEATURE [PartDesign::Chamfer] Chamfer019  label="M3 Nut Smooth Hole009"
  Base = -> Groove009 [Edge24,Edge23]
  BaseFeature = -> Groove009
  Size = 0.2
FEATURE [Sketcher::SketchObject] Sketch257
  MapMode = 5
  Support = -> [XY_Plane075]
  sketch-geometry (8):
    g0: LineSegment StartX=0 StartY=2.3094 StartZ=0 EndX=-2 EndY=1.1547 EndZ=0
    g1: LineSegment StartX=-2 StartY=1.1547 StartZ=0 EndX=-2 EndY=-1.1547 EndZ=0
    g2: LineSegment StartX=-2 StartY=-1.1547 StartZ=0 EndX=-2e-16 EndY=-2.3094 EndZ=0
    g3: LineSegment StartX=-2e-16 StartY=-2.3094 StartZ=0 EndX=2 EndY=-1.1547 EndZ=0
    g4: LineSegment StartX=2 StartY=-1.1547 StartZ=0 EndX=2 EndY=1.1547 EndZ=0
    g5: LineSegment StartX=2 StartY=1.1547 StartZ=0 EndX=0 EndY=2.3094 EndZ=0
    g6: Circle [constr] CenterX=0 CenterY=0 CenterZ=0 NormalX=0 NormalY=0 NormalZ=1 AngleXU=0 Radius=2.3094
    g7: Circle CenterX=0 CenterY=0 CenterZ=0 NormalX=0 NormalY=0 NormalZ=1 AngleXU=0 Radius=1
  constraints (18):
    c: Coincident(g0,g1)
    c: Coincident(g1,g2)
    c: Coincident(g2,g3)
    c: Coincident(g3,g4)
    c: Coincident(g4,g5)
    c: Coincident(g5,g0)
    c: Equal(g0, g1-g5) x5
    c: PointOnObject(g0,g6)
    c: PointOnObject(g1,g6)
    c: PointOnObject(g2,g6)
    c: PointOnObject(g3,g6)
    c: PointOnObject(g4,g6)
    c: PointOnObject(g5,g6)
    c: Coincident(g6,g-1)
    c: PointOnObject(g5,g-2)
    c: DistanceX(g0,g4) = 4
    c: Coincident(g7,g-1)
    c: Radius(g7) = 1
FEATURE [PartDesign::Pad] Pad084  label="M3 Nut Primitive009"
  Length = 0.6
  Length2 = 0.6
  Profile = -> Sketch257
  Type = 4
FEATURE [Sketcher::SketchObject] Sketch258
  MapMode = 5
  Support = -> [XY_Plane061]
  sketch-geometry (1):
    g0: Circle CenterX=0 CenterY=0 CenterZ=0 NormalX=0 NormalY=0 NormalZ=1 AngleXU=0 Radius=1.9
  constraints (2):
    c: Coincident(g0,g-1)
    c: Radius(g0) = 1.9
FEATURE [PartDesign::Pad] Pad082  label="M3x8 Head009"
  Length = 2
  Length2 = 100
  Profile = -> Sketch258
  Type = 0
FEATURE [Sketcher::SketchObject] Sketch259
  MapMode = 5
  Support = -> [XY_Plane060]
FEATURE [Sketcher::SketchObject] Sketch260
  MapMode = 5
  Support = -> [XY_Plane058]
FEATURE [Sketcher::SketchObject] Sketch261
  MapMode = 5
  Support = -> [XY_Plane060]
FEATURE [PartDesign::Body] Body037  label="M2 Nut006"
  Group = -> [Sketch256,Pad086,Sketch254,Groove009,Chamfer019,Sketch261,Sketch259]
  Origin = -> Origin060
  Placement = pos=(0,0,2.75) rot=(0,0,1;0rad)
  Tip = -> Chamfer019
FEATURE [Sketcher::SketchObject] Sketch262
  MapMode = 5
  Support = -> [XY_Plane076]
  sketch-geometry (1):
    g0: Circle CenterX=0 CenterY=0 CenterZ=0 NormalX=0 NormalY=0 NormalZ=1 AngleXU=0 Radius=1.9
  constraints (2):
    c: Coincident(g0,g-1)
    c: Radius(g0) = 1.9
FEATURE [PartDesign::Pad] Pad080  label="M3x8 Head008"
  Length = 2
  Length2 = 100
  Profile = -> Sketch262
  Type = 0
FEATURE [Sketcher::SketchObject] Sketch263
  MapMode = 5
  Placement = pos=(0,0,2) rot=(0,0,1;0rad)
  Support = -> [Pad082]
  sketch-geometry (1):
    g0: Circle CenterX=0 CenterY=0 CenterZ=0 NormalX=0 NormalY=0 NormalZ=1 AngleXU=0 Radius=1
  constraints (2):
    c: Coincident(g0,g-1)
    c: Radius(g0) = 1
FEATURE [PartDesign::Pad] Pad085  label="M3x8 Thread010"
  BaseFeature = -> Pad082
  Length = 8
  Length2 = 100
  Profile = -> Sketch263
  Type = 0
FEATURE [Sketcher::SketchObject] Sketch264
  MapMode = 5
  Placement = pos=(0,0,0) rot=(1,0,0;3.14159rad)
  Support = -> [Pad085]
  sketch-geometry (7):
    g0: LineSegment StartX=0.77 StartY=0.44456 StartZ=0 EndX=0 EndY=0.889119 EndZ=0
    g1: LineSegment StartX=0 StartY=0.889119 StartZ=0 EndX=-0.77 EndY=0.44456 EndZ=0
    g2: LineSegment StartX=-0.77 StartY=0.44456 StartZ=0 EndX=-0.77 EndY=-0.44456 EndZ=0
    g3: LineSegment StartX=-0.77 StartY=-0.44456 StartZ=0 EndX=3.85628e-11 EndY=-0.889119 EndZ=0
    g4: LineSegment StartX=3.85628e-11 StartY=-0.889119 StartZ=0 EndX=0.77 EndY=-0.44456 EndZ=0
    g5: LineSegment StartX=0.77 StartY=-0.44456 StartZ=0 EndX=0.77 EndY=0.44456 EndZ=0
    g6: Circle [constr] CenterX=0 CenterY=0 CenterZ=0 NormalX=0 NormalY=0 NormalZ=1 AngleXU=0 Radius=0.889119
  constraints (16):
    c: Coincident(g0,g1)
    c: Coincident(g1,g2)
    c: Coincident(g2,g3)
    c: Coincident(g3,g4)
    c: Coincident(g4,g5)
    c: Coincident(g5,g0)
    c: Equal(g0, g1-g5) x5
    c: PointOnObject(g0,g6)
    c: PointOnObject(g1,g6)
    c: PointOnObject(g2,g6)
    c: PointOnObject(g3,g6)
    c: PointOnObject(g4,g6)
    c: PointOnObject(g5,g6)
    c: Coincident(g6,g-1)
    c: PointOnObject(g0,g-2)
    c: DistanceX(g1,g0) = 1.54
FEATURE [PartDesign::Pocket] Pocket131  label="M3x8 Wrench009"
  BaseFeature = -> Pad085
  Length = 1
  Length2 = 100
  Profile = -> Sketch264
  Type = 0
FEATURE [PartDesign::Chamfer] Chamfer024  label="M3x8 Smooth011"
  Base = -> Pocket131 [Face11,Edge2,Edge24,Edge3]
  BaseFeature = -> Pocket131
  Size = 0.2
FEATURE [Sketcher::SketchObject] Sketch265
  MapMode = 5
  Support = -> [XY_Plane058]
  sketch-geometry (8):
    g0: LineSegment StartX=0 StartY=2.3094 StartZ=0 EndX=-2 EndY=1.1547 EndZ=0
    g1: LineSegment StartX=-2 StartY=1.1547 StartZ=0 EndX=-2 EndY=-1.1547 EndZ=0
    g2: LineSegment StartX=-2 StartY=-1.1547 StartZ=0 EndX=-2e-16 EndY=-2.3094 EndZ=0
    g3: LineSegment StartX=-2e-16 StartY=-2.3094 StartZ=0 EndX=2 EndY=-1.1547 EndZ=0
    g4: LineSegment StartX=2 StartY=-1.1547 StartZ=0 EndX=2 EndY=1.1547 EndZ=0
    g5: LineSegment StartX=2 StartY=1.1547 StartZ=0 EndX=0 EndY=2.3094 EndZ=0
    g6: Circle [constr] CenterX=0 CenterY=0 CenterZ=0 NormalX=0 NormalY=0 NormalZ=1 AngleXU=0 Radius=2.3094
    g7: Circle CenterX=0 CenterY=0 CenterZ=0 NormalX=0 NormalY=0 NormalZ=1 AngleXU=0 Radius=1
  constraints (18):
    c: Coincident(g0,g1)
    c: Coincident(g1,g2)
    c: Coincident(g2,g3)
    c: Coincident(g3,g4)
    c: Coincident(g4,g5)
    c: Coincident(g5,g0)
    c: Equal(g0, g1-g5) x5
    c: PointOnObject(g0,g6)
    c: PointOnObject(g1,g6)
    c: PointOnObject(g2,g6)
    c: PointOnObject(g3,g6)
    c: PointOnObject(g4,g6)
    c: PointOnObject(g5,g6)
    c: Coincident(g6,g-1)
    c: PointOnObject(g5,g-2)
    c: DistanceX(g0,g4) = 4
    c: Coincident(g7,g-1)
    c: Radius(g7) = 1
FEATURE [PartDesign::Pad] Pad076  label="M3 Nut Primitive007"
  Length = 0.6
  Length2 = 0.6
  Profile = -> Sketch265
  Type = 4
FEATURE [Sketcher::SketchObject] Sketch255
  ExternalGeometry = -> [Pad076]
  MapMode = 5
  Placement = pos=(0,0,0) rot=(0.57735,0.57735,0.57735;2.0944rad)
  Support = -> [YZ_Plane057]
  sketch-geometry (6):
    g0: LineSegment StartX=-1.9594 StartY=0.6 StartZ=0 EndX=-2.8094 EndY=0.6 EndZ=0
    g1: LineSegment StartX=-2.8094 StartY=0.6 StartZ=0 EndX=-2.8094 EndY=-0.6 EndZ=0
    g2: LineSegment StartX=-2.8094 StartY=-0.6 StartZ=0 EndX=-1.9594 EndY=-0.6 EndZ=0
    g3: LineSegment StartX=-1.9594 StartY=-0.6 StartZ=0 EndX=-2.3094 EndY=-0.4 EndZ=0
    g4: LineSegment StartX=-2.3094 StartY=-0.4 StartZ=0 EndX=-2.3094 EndY=0.4 EndZ=0
    g5: LineSegment StartX=-2.3094 StartY=0.4 StartZ=0 EndX=-1.9594 EndY=0.6 EndZ=0
  constraints (15):
    c: Horizontal(g0)
    c: Coincident(g0,g1)
    c: Coincident(g1,g2)
    c: Coincident(g2,g3)
    c: Coincident(g3,g4)
    c: Coincident(g4,g5)
    c: Coincident(g5,g0)
    c: Symmetric(g4,g3,g-1)
    c: Symmetric(g0,g2,g-1)
    c: Symmetric(g1,g0,g-1)
    c: DistanceX(g0,g4) = 0.5
    c: DistanceY(g3,g4) = 0.8
    c: DistanceY(g1,g0) = 1.2
    c: PointOnObject(g3,g-3)
    c: DistanceX(g4,g0) = 0.35
FEATURE [PartDesign::Groove] Groove008  label="M3 Nut Smooth008"
  Angle = 360
  Axis = (-2e-16,3e-16,1)
  Base = (0,0,0)
  BaseFeature = -> Pad076
  Profile = -> Sketch255
  ReferenceAxis = -> Sketch255 [V_Axis]
  Reversed = true
FEATURE [PartDesign::Chamfer] Chamfer023  label="M3 Nut Smooth Hole011"
  Base = -> Groove008 [Edge24,Edge23]
  BaseFeature = -> Groove008
  Size = 0.2
FEATURE [Sketcher::SketchObject] Sketch267
  MapMode = 5
  Placement = pos=(0,0,2) rot=(0,0,1;0rad)
  Support = -> [Pad080]
  sketch-geometry (1):
    g0: Circle CenterX=0 CenterY=0 CenterZ=0 NormalX=0 NormalY=0 NormalZ=1 AngleXU=0 Radius=1
  constraints (2):
    c: Coincident(g0,g-1)
    c: Radius(g0) = 1
FEATURE [PartDesign::Pad] Pad081  label="M3x8 Thread008"
  BaseFeature = -> Pad080
  Length = 8
  Length2 = 100
  Profile = -> Sketch267
  Type = 0
FEATURE [Sketcher::SketchObject] Sketch266
  MapMode = 5
  Placement = pos=(0,0,0) rot=(1,0,0;3.14159rad)
  Support = -> [Pad081]
  sketch-geometry (7):
    g0: LineSegment StartX=0.77 StartY=0.44456 StartZ=0 EndX=0 EndY=0.889119 EndZ=0
    g1: LineSegment StartX=0 StartY=0.889119 StartZ=0 EndX=-0.77 EndY=0.44456 EndZ=0
    g2: LineSegment StartX=-0.77 StartY=0.44456 StartZ=0 EndX=-0.77 EndY=-0.44456 EndZ=0
    g3: LineSegment StartX=-0.77 StartY=-0.44456 StartZ=0 EndX=3.85628e-11 EndY=-0.889119 EndZ=0
    g4: LineSegment StartX=3.85628e-11 StartY=-0.889119 StartZ=0 EndX=0.77 EndY=-0.44456 EndZ=0
    g5: LineSegment StartX=0.77 StartY=-0.44456 StartZ=0 EndX=0.77 EndY=0.44456 EndZ=0
    g6: Circle [constr] CenterX=0 CenterY=0 CenterZ=0 NormalX=0 NormalY=0 NormalZ=1 AngleXU=0 Radius=0.889119
  constraints (16):
    c: Coincident(g0,g1)
    c: Coincident(g1,g2)
    c: Coincident(g2,g3)
    c: Coincident(g3,g4)
    c: Coincident(g4,g5)
    c: Coincident(g5,g0)
    c: Equal(g0, g1-g5) x5
    c: PointOnObject(g0,g6)
    c: PointOnObject(g1,g6)
    c: PointOnObject(g2,g6)
    c: PointOnObject(g3,g6)
    c: PointOnObject(g4,g6)
    c: PointOnObject(g5,g6)
    c: Coincident(g6,g-1)
    c: PointOnObject(g0,g-2)
    c: DistanceX(g1,g0) = 1.54
FEATURE [PartDesign::Pocket] Pocket132  label="M3x8 Wrench010"
  BaseFeature = -> Pad081
  Length = 1
  Length2 = 100
  Profile = -> Sketch266
  Type = 0
FEATURE [PartDesign::Chamfer] Chamfer020  label="M3x8 Smooth009"
  Base = -> Pocket132 [Face11,Edge2,Edge24,Edge3]
  BaseFeature = -> Pocket132
  Size = 0.2
FEATURE [PartDesign::Body] Body038  label="M2x014"
  Group = -> [Sketch262,Pad080,Sketch267,Pad081,Sketch266,Pocket132,Chamfer020]
  Origin = -> Origin068
  Tip = -> Chamfer020
FEATURE [App::Part] Part016  label="M010"
  Group = -> [Body038,Body037]
  Origin = -> Origin059
  Placement = pos=(-9.1,-5.25,80) rot=(0,1,0;3.14159rad)
FEATURE [Sketcher::SketchObject] Sketch268
  ExternalGeometry = -> [Pad084]
  MapMode = 5
  Placement = pos=(0,0,0) rot=(0.57735,0.57735,0.57735;2.0944rad)
  Support = -> [YZ_Plane073]
  sketch-geometry (6):
    g0: LineSegment StartX=-1.9594 StartY=0.6 StartZ=0 EndX=-2.8094 EndY=0.6 EndZ=0
    g1: LineSegment StartX=-2.8094 StartY=0.6 StartZ=0 EndX=-2.8094 EndY=-0.6 EndZ=0
    g2: LineSegment StartX=-2.8094 StartY=-0.6 StartZ=0 EndX=-1.9594 EndY=-0.6 EndZ=0
    g3: LineSegment StartX=-1.9594 StartY=-0.6 StartZ=0 EndX=-2.3094 EndY=-0.4 EndZ=0
    g4: LineSegment StartX=-2.3094 StartY=-0.4 StartZ=0 EndX=-2.3094 EndY=0.4 EndZ=0
    g5: LineSegment StartX=-2.3094 StartY=0.4 StartZ=0 EndX=-1.9594 EndY=0.6 EndZ=0
  constraints (15):
    c: Horizontal(g0)
    c: Coincident(g0,g1)
    c: Coincident(g1,g2)
    c: Coincident(g2,g3)
    c: Coincident(g3,g4)
    c: Coincident(g4,g5)
    c: Coincident(g5,g0)
    c: Symmetric(g4,g3,g-1)
    c: Symmetric(g0,g2,g-1)
    c: Symmetric(g1,g0,g-1)
    c: DistanceX(g0,g4) = 0.5
    c: DistanceY(g3,g4) = 0.8
    c: DistanceY(g1,g0) = 1.2
    c: PointOnObject(g3,g-3)
    c: DistanceX(g4,g0) = 0.35
FEATURE [PartDesign::Groove] Groove010  label="M3 Nut Smooth010"
  Angle = 360
  Axis = (-2e-16,3e-16,1)
  Base = (0,0,0)
  BaseFeature = -> Pad084
  Profile = -> Sketch268
  ReferenceAxis = -> Sketch268 [V_Axis]
  Reversed = true
FEATURE [PartDesign::Chamfer] Chamfer026  label="M3 Nut Smooth Hole012"
  Base = -> Groove010 [Edge24,Edge23]
  BaseFeature = -> Groove010
  Size = 0.2
FEATURE [Sketcher::SketchObject] Sketch271
  MapMode = 5
  Support = -> [XY_Plane072]
  sketch-geometry (8):
    g0: LineSegment StartX=0 StartY=2.3094 StartZ=0 EndX=-2 EndY=1.1547 EndZ=0
    g1: LineSegment StartX=-2 StartY=1.1547 StartZ=0 EndX=-2 EndY=-1.1547 EndZ=0
    g2: LineSegment StartX=-2 StartY=-1.1547 StartZ=0 EndX=-2e-16 EndY=-2.3094 EndZ=0
    g3: LineSegment StartX=-2e-16 StartY=-2.3094 StartZ=0 EndX=2 EndY=-1.1547 EndZ=0
    g4: LineSegment StartX=2 StartY=-1.1547 StartZ=0 EndX=2 EndY=1.1547 EndZ=0
    g5: LineSegment StartX=2 StartY=1.1547 StartZ=0 EndX=0 EndY=2.3094 EndZ=0
    g6: Circle [constr] CenterX=0 CenterY=0 CenterZ=0 NormalX=0 NormalY=0 NormalZ=1 AngleXU=0 Radius=2.3094
    g7: Circle CenterX=0 CenterY=0 CenterZ=0 NormalX=0 NormalY=0 NormalZ=1 AngleXU=0 Radius=1
  constraints (18):
    c: Coincident(g0,g1)
    c: Coincident(g1,g2)
    c: Coincident(g2,g3)
    c: Coincident(g3,g4)
    c: Coincident(g4,g5)
    c: Coincident(g5,g0)
    c: Equal(g0, g1-g5) x5
    c: PointOnObject(g0,g6)
    c: PointOnObject(g1,g6)
    c: PointOnObject(g2,g6)
    c: PointOnObject(g3,g6)
    c: PointOnObject(g4,g6)
    c: PointOnObject(g5,g6)
    c: Coincident(g6,g-1)
    c: PointOnObject(g5,g-2)
    c: DistanceX(g0,g4) = 4
    c: Coincident(g7,g-1)
    c: Radius(g7) = 1
FEATURE [PartDesign::Pad] Pad091  label="M3 Nut Primitive011"
  Length = 0.6
  Length2 = 0.6
  Profile = -> Sketch271
  Type = 4
FEATURE [Sketcher::SketchObject] Sketch270
  ExternalGeometry = -> [Pad091]
  MapMode = 5
  Placement = pos=(0,0,0) rot=(0.57735,0.57735,0.57735;2.0944rad)
  Support = -> [YZ_Plane067]
  sketch-geometry (6):
    g0: LineSegment StartX=-1.9594 StartY=0.6 StartZ=0 EndX=-2.8094 EndY=0.6 EndZ=0
    g1: LineSegment StartX=-2.8094 StartY=0.6 StartZ=0 EndX=-2.8094 EndY=-0.6 EndZ=0
    g2: LineSegment StartX=-2.8094 StartY=-0.6 StartZ=0 EndX=-1.9594 EndY=-0.6 EndZ=0
    g3: LineSegment StartX=-1.9594 StartY=-0.6 StartZ=0 EndX=-2.3094 EndY=-0.4 EndZ=0
    g4: LineSegment StartX=-2.3094 StartY=-0.4 StartZ=0 EndX=-2.3094 EndY=0.4 EndZ=0
    g5: LineSegment StartX=-2.3094 StartY=0.4 StartZ=0 EndX=-1.9594 EndY=0.6 EndZ=0
  constraints (15):
    c: Horizontal(g0)
    c: Coincident(g0,g1)
    c: Coincident(g1,g2)
    c: Coincident(g2,g3)
    c: Coincident(g3,g4)
    c: Coincident(g4,g5)
    c: Coincident(g5,g0)
    c: Symmetric(g4,g3,g-1)
    c: Symmetric(g0,g2,g-1)
    c: Symmetric(g1,g0,g-1)
    c: DistanceX(g0,g4) = 0.5
    c: DistanceY(g3,g4) = 0.8
    c: DistanceY(g1,g0) = 1.2
    c: PointOnObject(g3,g-3)
    c: DistanceX(g4,g0) = 0.35
FEATURE [PartDesign::Groove] Groove011  label="M3 Nut Smooth011"
  Angle = 360
  Axis = (-2e-16,3e-16,1)
  Base = (0,0,0)
  BaseFeature = -> Pad091
  Profile = -> Sketch270
  ReferenceAxis = -> Sketch270 [V_Axis]
  Reversed = true
FEATURE [PartDesign::Chamfer] Chamfer016  label="M3 Nut Smooth Hole007"
  Base = -> Groove011 [Edge24,Edge23]
  BaseFeature = -> Groove011
  Size = 0.2
FEATURE [Sketcher::SketchObject] Sketch273
  MapMode = 5
  Support = -> [XY_Plane068]
  sketch-geometry (1):
    g0: Circle CenterX=0 CenterY=0 CenterZ=0 NormalX=0 NormalY=0 NormalZ=1 AngleXU=0 Radius=1.9
  constraints (2):
    c: Coincident(g0,g-1)
    c: Radius(g0) = 1.9
FEATURE [PartDesign::Pad] Pad087  label="M3x8 Head010"
  Length = 2
  Length2 = 100
  Profile = -> Sketch273
  Type = 0
FEATURE [Sketcher::SketchObject] Sketch269
  MapMode = 5
  Placement = pos=(0,0,2) rot=(0,0,1;0rad)
  Support = -> [Pad087]
  sketch-geometry (1):
    g0: Circle CenterX=0 CenterY=0 CenterZ=0 NormalX=0 NormalY=0 NormalZ=1 AngleXU=0 Radius=1
  constraints (2):
    c: Coincident(g0,g-1)
    c: Radius(g0) = 1
FEATURE [PartDesign::Pad] Pad083  label="M3x8 Thread009"
  BaseFeature = -> Pad087
  Length = 8
  Length2 = 100
  Profile = -> Sketch269
  Type = 0
FEATURE [Sketcher::SketchObject] Sketch276
  MapMode = 5
  Placement = pos=(0,0,0) rot=(1,0,0;3.14159rad)
  Support = -> [Pad083]
  sketch-geometry (7):
    g0: LineSegment StartX=0.77 StartY=0.44456 StartZ=0 EndX=0 EndY=0.889119 EndZ=0
    g1: LineSegment StartX=0 StartY=0.889119 StartZ=0 EndX=-0.77 EndY=0.44456 EndZ=0
    g2: LineSegment StartX=-0.77 StartY=0.44456 StartZ=0 EndX=-0.77 EndY=-0.44456 EndZ=0
    g3: LineSegment StartX=-0.77 StartY=-0.44456 StartZ=0 EndX=3.85628e-11 EndY=-0.889119 EndZ=0
    g4: LineSegment StartX=3.85628e-11 StartY=-0.889119 StartZ=0 EndX=0.77 EndY=-0.44456 EndZ=0
    g5: LineSegment StartX=0.77 StartY=-0.44456 StartZ=0 EndX=0.77 EndY=0.44456 EndZ=0
    g6: Circle [constr] CenterX=0 CenterY=0 CenterZ=0 NormalX=0 NormalY=0 NormalZ=1 AngleXU=0 Radius=0.889119
  constraints (16):
    c: Coincident(g0,g1)
    c: Coincident(g1,g2)
    c: Coincident(g2,g3)
    c: Coincident(g3,g4)
    c: Coincident(g4,g5)
    c: Coincident(g5,g0)
    c: Equal(g0, g1-g5) x5
    c: PointOnObject(g0,g6)
    c: PointOnObject(g1,g6)
    c: PointOnObject(g2,g6)
    c: PointOnObject(g3,g6)
    c: PointOnObject(g4,g6)
    c: PointOnObject(g5,g6)
    c: Coincident(g6,g-1)
    c: PointOnObject(g0,g-2)
    c: DistanceX(g1,g0) = 1.54
FEATURE [PartDesign::Pocket] Pocket128  label="M3x8 Wrench007"
  BaseFeature = -> Pad083
  Length = 1
  Length2 = 100
  Profile = -> Sketch276
  Type = 0
FEATURE [PartDesign::Chamfer] Chamfer021  label="M3x8 Smooth010"
  Base = -> Pocket128 [Face11,Edge2,Edge24,Edge3]
  BaseFeature = -> Pocket128
  Size = 0.2
FEATURE [PartDesign::Body] Body040  label="M2x015"
  Group = -> [Sketch273,Pad087,Sketch269,Pad083,Sketch276,Pocket128,Chamfer021]
  Origin = -> Origin066
  Tip = -> Chamfer021
FEATURE [Sketcher::SketchObject] Sketch277
  MapMode = 5
  Support = -> [XY_Plane075]
FEATURE [Sketcher::SketchObject] Sketch278
  MapMode = 5
  Support = -> [XY_Plane071]
  sketch-geometry (1):
    g0: Circle CenterX=0 CenterY=0 CenterZ=0 NormalX=0 NormalY=0 NormalZ=1 AngleXU=0 Radius=1.9
  constraints (2):
    c: Coincident(g0,g-1)
    c: Radius(g0) = 1.9
FEATURE [PartDesign::Pad] Pad088  label="M3x8 Head011"
  Length = 2
  Length2 = 100
  Profile = -> Sketch278
  Type = 0
FEATURE [Sketcher::SketchObject] Sketch272
  MapMode = 5
  Placement = pos=(0,0,2) rot=(0,0,1;0rad)
  Support = -> [Pad088]
  sketch-geometry (1):
    g0: Circle CenterX=0 CenterY=0 CenterZ=0 NormalX=0 NormalY=0 NormalZ=1 AngleXU=0 Radius=1
  constraints (2):
    c: Coincident(g0,g-1)
    c: Radius(g0) = 1
FEATURE [PartDesign::Pad] Pad090  label="M3x8 Thread011"
  BaseFeature = -> Pad088
  Length = 8
  Length2 = 100
  Profile = -> Sketch272
  Type = 0
FEATURE [Sketcher::SketchObject] Sketch274
  MapMode = 5
  Placement = pos=(0,0,0) rot=(1,0,0;3.14159rad)
  Support = -> [Pad090]
  sketch-geometry (7):
    g0: LineSegment StartX=0.77 StartY=0.44456 StartZ=0 EndX=0 EndY=0.889119 EndZ=0
    g1: LineSegment StartX=0 StartY=0.889119 StartZ=0 EndX=-0.77 EndY=0.44456 EndZ=0
    g2: LineSegment StartX=-0.77 StartY=0.44456 StartZ=0 EndX=-0.77 EndY=-0.44456 EndZ=0
    g3: LineSegment StartX=-0.77 StartY=-0.44456 StartZ=0 EndX=3.85628e-11 EndY=-0.889119 EndZ=0
    g4: LineSegment StartX=3.85628e-11 StartY=-0.889119 StartZ=0 EndX=0.77 EndY=-0.44456 EndZ=0
    g5: LineSegment StartX=0.77 StartY=-0.44456 StartZ=0 EndX=0.77 EndY=0.44456 EndZ=0
    g6: Circle [constr] CenterX=0 CenterY=0 CenterZ=0 NormalX=0 NormalY=0 NormalZ=1 AngleXU=0 Radius=0.889119
  constraints (16):
    c: Coincident(g0,g1)
    c: Coincident(g1,g2)
    c: Coincident(g2,g3)
    c: Coincident(g3,g4)
    c: Coincident(g4,g5)
    c: Coincident(g5,g0)
    c: Equal(g0, g1-g5) x5
    c: PointOnObject(g0,g6)
    c: PointOnObject(g1,g6)
    c: PointOnObject(g2,g6)
    c: PointOnObject(g3,g6)
    c: PointOnObject(g4,g6)
    c: PointOnObject(g5,g6)
    c: Coincident(g6,g-1)
    c: PointOnObject(g0,g-2)
    c: DistanceX(g1,g0) = 1.54
FEATURE [PartDesign::Pocket] Pocket133  label="M3x8 Wrench011"
  BaseFeature = -> Pad090
  Length = 1
  Length2 = 100
  Profile = -> Sketch274
  Type = 0
FEATURE [PartDesign::Chamfer] Chamfer018  label="M3x8 Smooth008"
  Base = -> Pocket133 [Face11,Edge2,Edge24,Edge3]
  BaseFeature = -> Pocket133
  Size = 0.2
FEATURE [Sketcher::SketchObject] Sketch279
  MapMode = 5
  Support = -> [XY_Plane075]
FEATURE [PartDesign::Body] Body039  label="M2 Nut007"
  Group = -> [Sketch257,Pad084,Sketch268,Groove010,Chamfer026,Sketch279,Sketch277]
  Origin = -> Origin065
  Placement = pos=(0,0,2.75) rot=(0,0,1;0rad)
  Tip = -> Chamfer026
FEATURE [App::Part] Part014  label="M008"
  Group = -> [Body040,Body039]
  Origin = -> Origin064
  Placement = pos=(9.1,-5.25,80) rot=(0,1,0;3.14159rad)
FEATURE [Sketcher::SketchObject] Sketch280
  MapMode = 5
  Support = -> [XY_Plane072]
FEATURE [Sketcher::SketchObject] Sketch282
  MapMode = 5
  Support = -> [XY_Plane072]
FEATURE [Sketcher::SketchObject] Sketch283
  MapMode = 5
  Support = -> [XY_Plane066]
  sketch-geometry (8):
    g0: LineSegment StartX=0 StartY=2.3094 StartZ=0 EndX=-2 EndY=1.1547 EndZ=0
    g1: LineSegment StartX=-2 StartY=1.1547 StartZ=0 EndX=-2 EndY=-1.1547 EndZ=0
    g2: LineSegment StartX=-2 StartY=-1.1547 StartZ=0 EndX=-2e-16 EndY=-2.3094 EndZ=0
    g3: LineSegment StartX=-2e-16 StartY=-2.3094 StartZ=0 EndX=2 EndY=-1.1547 EndZ=0
    g4: LineSegment StartX=2 StartY=-1.1547 StartZ=0 EndX=2 EndY=1.1547 EndZ=0
    g5: LineSegment StartX=2 StartY=1.1547 StartZ=0 EndX=0 EndY=2.3094 EndZ=0
    g6: Circle [constr] CenterX=0 CenterY=0 CenterZ=0 NormalX=0 NormalY=0 NormalZ=1 AngleXU=0 Radius=2.3094
    g7: Circle CenterX=0 CenterY=0 CenterZ=0 NormalX=0 NormalY=0 NormalZ=1 AngleXU=0 Radius=1
  constraints (18):
    c: Coincident(g0,g1)
    c: Coincident(g1,g2)
    c: Coincident(g2,g3)
    c: Coincident(g3,g4)
    c: Coincident(g4,g5)
    c: Coincident(g5,g0)
    c: Equal(g0, g1-g5) x5
    c: PointOnObject(g0,g6)
    c: PointOnObject(g1,g6)
    c: PointOnObject(g2,g6)
    c: PointOnObject(g3,g6)
    c: PointOnObject(g4,g6)
    c: PointOnObject(g5,g6)
    c: Coincident(g6,g-1)
    c: PointOnObject(g5,g-2)
    c: DistanceX(g0,g4) = 4
    c: Coincident(g7,g-1)
    c: Radius(g7) = 1
FEATURE [PartDesign::Pad] Pad092  label="M3 Nut Primitive012"
  Length = 0.6
  Length2 = 0.6
  Profile = -> Sketch283
  Type = 4
FEATURE [Sketcher::SketchObject] Sketch281
  ExternalGeometry = -> [Pad092]
  MapMode = 5
  Placement = pos=(0,0,0) rot=(0.57735,0.57735,0.57735;2.0944rad)
  Support = -> [YZ_Plane064]
  sketch-geometry (6):
    g0: LineSegment StartX=-1.9594 StartY=0.6 StartZ=0 EndX=-2.8094 EndY=0.6 EndZ=0
    g1: LineSegment StartX=-2.8094 StartY=0.6 StartZ=0 EndX=-2.8094 EndY=-0.6 EndZ=0
    g2: LineSegment StartX=-2.8094 StartY=-0.6 StartZ=0 EndX=-1.9594 EndY=-0.6 EndZ=0
    g3: LineSegment StartX=-1.9594 StartY=-0.6 StartZ=0 EndX=-2.3094 EndY=-0.4 EndZ=0
    g4: LineSegment StartX=-2.3094 StartY=-0.4 StartZ=0 EndX=-2.3094 EndY=0.4 EndZ=0
    g5: LineSegment StartX=-2.3094 StartY=0.4 StartZ=0 EndX=-1.9594 EndY=0.6 EndZ=0
  constraints (15):
    c: Horizontal(g0)
    c: Coincident(g0,g1)
    c: Coincident(g1,g2)
    c: Coincident(g2,g3)
    c: Coincident(g3,g4)
    c: Coincident(g4,g5)
    c: Coincident(g5,g0)
    c: Symmetric(g4,g3,g-1)
    c: Symmetric(g0,g2,g-1)
    c: Symmetric(g1,g0,g-1)
    c: DistanceX(g0,g4) = 0.5
    c: DistanceY(g3,g4) = 0.8
    c: DistanceY(g1,g0) = 1.2
    c: PointOnObject(g3,g-3)
    c: DistanceX(g4,g0) = 0.35
FEATURE [PartDesign::Groove] Groove012  label="M3 Nut Smooth012"
  Angle = 360
  Axis = (-2e-16,3e-16,1)
  Base = (0,0,0)
  BaseFeature = -> Pad092
  Profile = -> Sketch281
  ReferenceAxis = -> Sketch281 [V_Axis]
  Reversed = true
FEATURE [PartDesign::Chamfer] Chamfer017  label="M3 Nut Smooth Hole008"
  Base = -> Groove012 [Edge24,Edge23]
  BaseFeature = -> Groove012
  Size = 0.2
FEATURE [Sketcher::SketchObject] Sketch285
  MapMode = 5
  Support = -> [XY_Plane065]
  sketch-geometry (1):
    g0: Circle CenterX=0 CenterY=0 CenterZ=0 NormalX=0 NormalY=0 NormalZ=1 AngleXU=0 Radius=1.9
  constraints (2):
    c: Coincident(g0,g-1)
    c: Radius(g0) = 1.9
FEATURE [PartDesign::Pad] Pad089  label="M3x8 Head012"
  Length = 2
  Length2 = 100
  Profile = -> Sketch285
  Type = 0
FEATURE [Sketcher::SketchObject] Sketch284
  MapMode = 5
  Placement = pos=(0,0,2) rot=(0,0,1;0rad)
  Support = -> [Pad089]
  sketch-geometry (1):
    g0: Circle CenterX=0 CenterY=0 CenterZ=0 NormalX=0 NormalY=0 NormalZ=1 AngleXU=0 Radius=1
  constraints (2):
    c: Coincident(g0,g-1)
    c: Radius(g0) = 1
FEATURE [PartDesign::Pad] Pad093  label="M3x8 Thread012"
  BaseFeature = -> Pad089
  Length = 8
  Length2 = 100
  Profile = -> Sketch284
  Type = 0
FEATURE [Sketcher::SketchObject] Sketch275
  MapMode = 5
  Placement = pos=(0,0,0) rot=(1,0,0;3.14159rad)
  Support = -> [Pad093]
  sketch-geometry (7):
    g0: LineSegment StartX=0.77 StartY=0.44456 StartZ=0 EndX=0 EndY=0.889119 EndZ=0
    g1: LineSegment StartX=0 StartY=0.889119 StartZ=0 EndX=-0.77 EndY=0.44456 EndZ=0
    g2: LineSegment StartX=-0.77 StartY=0.44456 StartZ=0 EndX=-0.77 EndY=-0.44456 EndZ=0
    g3: LineSegment StartX=-0.77 StartY=-0.44456 StartZ=0 EndX=3.85628e-11 EndY=-0.889119 EndZ=0
    g4: LineSegment StartX=3.85628e-11 StartY=-0.889119 StartZ=0 EndX=0.77 EndY=-0.44456 EndZ=0
    g5: LineSegment StartX=0.77 StartY=-0.44456 StartZ=0 EndX=0.77 EndY=0.44456 EndZ=0
    g6: Circle [constr] CenterX=0 CenterY=0 CenterZ=0 NormalX=0 NormalY=0 NormalZ=1 AngleXU=0 Radius=0.889119
  constraints (16):
    c: Coincident(g0,g1)
    c: Coincident(g1,g2)
    c: Coincident(g2,g3)
    c: Coincident(g3,g4)
    c: Coincident(g4,g5)
    c: Coincident(g5,g0)
    c: Equal(g0, g1-g5) x5
    c: PointOnObject(g0,g6)
    c: PointOnObject(g1,g6)
    c: PointOnObject(g2,g6)
    c: PointOnObject(g3,g6)
    c: PointOnObject(g4,g6)
    c: PointOnObject(g5,g6)
    c: Coincident(g6,g-1)
    c: PointOnObject(g0,g-2)
    c: DistanceX(g1,g0) = 1.54
FEATURE [PartDesign::Pocket] Pocket134  label="M3x8 Wrench012"
  BaseFeature = -> Pad093
  Length = 1
  Length2 = 100
  Profile = -> Sketch275
  Type = 0
FEATURE [PartDesign::Chamfer] Chamfer015  label="M3x8 Smooth007"
  Base = -> Pocket134 [Face11,Edge2,Edge24,Edge3]
  BaseFeature = -> Pocket134
  Size = 0.2
FEATURE [PartDesign::Body] Body043  label="M2x016"
  Group = -> [Sketch249,Pad078,Sketch250,Pad079,Sketch246,Pocket129,Chamfer025]
  Origin = -> Origin073
  Tip = -> Chamfer025
FEATURE [PartDesign::Body] Body044  label="M2 Nut008"
  Group = -> [Sketch252,Pad077,Sketch248,Groove007,Chamfer022,Sketch247,Sketch251]
  Origin = -> Origin074
  Placement = pos=(0,0,2.75) rot=(0,0,1;0rad)
  Tip = -> Chamfer022
FEATURE [App::Part] Part018  label="M011"
  Group = -> [Body043,Body044]
  Origin = -> Origin061
  Placement = pos=(-9.8e-15,10.5,80) rot=(0,1,0;3.14159rad)
FEATURE [PartDesign::Body] Body045  label="M2 Nut009"
  Group = -> [Sketch265,Pad076,Sketch255,Groove008,Chamfer023,Sketch253,Sketch260]
  Origin = -> Origin058
  Placement = pos=(0,0,2.75) rot=(0,0,1;0rad)
  Tip = -> Chamfer023
FEATURE [PartDesign::Body] Body046  label="M2x017"
  Group = -> [Sketch258,Pad082,Sketch263,Pad085,Sketch264,Pocket131,Chamfer024]
  Origin = -> Origin062
  Tip = -> Chamfer024
FEATURE [App::Part] Part019  label="M012"
  Group = -> [Body046,Body045]
  Origin = -> Origin057
  Placement = pos=(-9.8e-15,-10.5,80) rot=(0,1,0;3.14159rad)
FEATURE [PartDesign::Body] Body048  label="M2x018"
  Group = -> [Sketch285,Pad089,Sketch284,Pad093,Sketch275,Pocket134,Chamfer015]
  Origin = -> Origin077
  Tip = -> Chamfer015
FEATURE [PartDesign::Body] Body049  label="M2 Nut011"
  Group = -> [Sketch271,Pad091,Sketch270,Groove011,Chamfer016,Sketch282,Sketch280]
  Origin = -> Origin069
  Placement = pos=(0,0,2.75) rot=(0,0,1;0rad)
  Tip = -> Chamfer016
FEATURE [PartDesign::Body] Body050  label="M2x019"
  Group = -> [Sketch278,Pad088,Sketch272,Pad090,Sketch274,Pocket133,Chamfer018]
  Origin = -> Origin063
  Tip = -> Chamfer018
FEATURE [App::Part] Part015  label="M009"
  Group = -> [Body050,Body049]
  Origin = -> Origin067
  Placement = pos=(9.1,5.25,80) rot=(0,1,0;3.14159rad)
FEATURE [Sketcher::SketchObject] Sketch286
  MapMode = 5
  Support = -> [XY_Plane066]
FEATURE [Sketcher::SketchObject] Sketch287
  MapMode = 5
  Support = -> [XY_Plane066]
FEATURE [PartDesign::Body] Body047  label="M2 Nut010"
  Group = -> [Sketch283,Pad092,Sketch281,Groove012,Chamfer017,Sketch287,Sketch286]
  Origin = -> Origin078
  Placement = pos=(0,0,2.75) rot=(0,0,1;0rad)
  Tip = -> Chamfer017
FEATURE [App::Part] Part021  label="M013"
  Group = -> [Body048,Body047]
  Origin = -> Origin079
  Placement = pos=(-9.1,5.25,80) rot=(0,1,0;3.14159rad)
FEATURE [App::Part] Part017  label="Screws001"
  Group = -> [Part018,Part019,Part016,Part014,Part015,Part021]
  Origin = -> Origin070
  Placement = pos=(0,0,-71) rot=(0,0,1;0rad)
FEATURE [App::Part] Part020  label="servohorn moun tpost"
  Group = -> [Body041,Part013,Part017]
  Origin = -> Origin076
  Placement = pos=(-144.1,-24.45,27.05) rot=(1,0,0;1.5708rad)
FEATURE [Sketcher::SketchObject] Sketch290
  MapMode = 5
  Support = -> [XY_Plane081]
  sketch-geometry (9):
    g0: ArcOfCircle CenterX=0 CenterY=0 CenterZ=0 NormalX=0 NormalY=0 NormalZ=1 AngleXU=0 Radius=16.5 StartAngle=3.66519 EndAngle=6.80678
    g1: LineSegment StartX=-14.2894 StartY=-8.25 StartZ=0 EndX=-27.2211 EndY=14.1484 EndZ=0
    g2: LineSegment StartX=1.3577 StartY=30.6484 StartZ=0 EndX=14.2894 EndY=8.25 EndZ=0
    g3: LineSegment [constr] StartX=-27.2211 StartY=14.1484 StartZ=0 EndX=1.3577 EndY=30.6484 EndZ=0
    g4: ArcOfCircle CenterX=-28.6962 CenterY=13.2968 CenterZ=0 NormalX=0 NormalY=0 NormalZ=1 AngleXU=0 Radius=1.70319 StartAngle=0.523599 EndAngle=1.5708
    g5: ArcOfCircle CenterX=-23.5 CenterY=16.2968 CenterZ=0 NormalX=0 NormalY=0 NormalZ=1 AngleXU=0 Radius=28.7032 StartAngle=0.523599 EndAngle=1.5708
    g6: LineSegment StartX=-28.6962 StartY=15 StartZ=0 EndX=-40 EndY=15 EndZ=0
    g7: LineSegment StartX=-40 StartY=15 StartZ=0 EndX=-40 EndY=45 EndZ=0
    g8: LineSegment StartX=-40 StartY=45 StartZ=0 EndX=-23.5 EndY=45 EndZ=0
  constraints (22):
    c: Coincident(g0,g-1)
    c: Tangent(g0,g1) = 1.5708
    c: Coincident(g3,g2) = -1.5708
    c: Parallel(g2,g1)
    c: Radius(g0) = 16.5
    c: Tangent(g2,g0) = 1.5708
    c: Coincident(g3,g1)
    c: Perpendicular(g1,g3)
    c: Tangent(g5,g2) = 1.5708
    c: Tangent(g4,g1) = -1.5708
    c: Horizontal(g6)
    c: Coincident(g7,g6)
    c: Vertical(g7)
    c: Coincident(g8,g7)
    c: Horizontal(g8)
    c: Tangent(g6,g4) = -1.5708
    c: DistanceY(g7,g7) = 30
    c: DistanceX(g6,g0) = 40
    c: DistanceX(g8,g8) = 16.5
    c: Tangent(g8,g5) = 1.5708
    c: DistanceY(g0,g4) = 15
    c: Angle(g3) = 0.523599
FEATURE [PartDesign::Pad] Pad094  label="Baseplate002"
  Length = 5
  Length2 = 100
  Profile = -> Sketch290
  Type = 0
FEATURE [Sketcher::SketchObject] Sketch289
  MapMode = 5
  Placement = pos=(-40,0,0) rot=(0.57735,-0.57735,-0.57735;2.0944rad)
  Support = -> [Pad094]
  sketch-geometry (4):
    g0: ArcOfCircle CenterX=-25 CenterY=-21 CenterZ=0 NormalX=0 NormalY=0 NormalZ=1 AngleXU=0 Radius=26 StartAngle=1.17601 EndAngle=1.5708
    g1: LineSegment StartX=-25 StartY=5 StartZ=0 EndX=-25 EndY=6 EndZ=0
    g2: LineSegment StartX=-25 StartY=6 StartZ=0 EndX=-15 EndY=6 EndZ=0
    g3: LineSegment StartX=-15 StartY=6 StartZ=0 EndX=-15 EndY=3 EndZ=0
  constraints (13):
    c: Coincident(g1,g0)
    c: Vertical(g1)
    c: Horizontal(g2)
    c: Coincident(g3,g2)
    c: Vertical(g3)
    c: Coincident(g0,g3)
    c: Coincident(g1,g2)
    c: DistanceY(g1,g1) = 1
    c: DistanceY(g3,g3) = 3
    c: DistanceX(g2,g2) = 10
    c: DistanceY(g-1,g0) = 5
    c: Perpendicular(g0,g1)
    c: DistanceX(g0,g-1) = 15
FEATURE [PartDesign::SubtractivePipe] SubtractivePipe002  label="Smooth Surfaces002"
  AuxilleryCurvelinear = true
  AuxillerySpineTangent = false
  BaseFeature = -> Pad094
  Binormal = (0,0,0)
  Mode = 0
  Profile = -> Sketch289
  Spine = -> Pad094 [Edge19,Edge22,Edge24,Edge4,Edge7,Edge10,Edge13]
  SpineTangent = false
  Transformation = 0
  Transition = 0
FEATURE [PartDesign::Fillet] Fillet045  label="Smooth Edges002"
  Base = -> SubtractivePipe002 [Edge21]
  BaseFeature = -> SubtractivePipe002
  Radius = 1.5
FEATURE [Sketcher::SketchObject] Sketch291
  MapMode = 5
  Placement = pos=(0,0,5) rot=(0,0,1;0rad)
  Support = -> [SubtractivePipe002]
  sketch-geometry (3):
    g0: Circle [constr] CenterX=0 CenterY=15 CenterZ=0 NormalX=0 NormalY=0 NormalZ=1 AngleXU=0 Radius=35
    g1: Circle CenterX=-33.541 CenterY=25 CenterZ=0 NormalX=0 NormalY=0 NormalZ=1 AngleXU=0 Radius=2.85
    g2: Circle CenterX=-28.7228 CenterY=35 CenterZ=0 NormalX=0 NormalY=0 NormalZ=1 AngleXU=0 Radius=2.85
  constraints (9):
    c: PointOnObject(g1,g0)
    c: PointOnObject(g2,g0)
    c: Radius(g0) = 35
    c: Equal(g2,g1)
    c: Radius(g1) = 2.85
    c: DistanceY(g1,g2) = 10
    c: DistanceY(g-1,g0) = 15
    c: DistanceY(g0,g1) = 10
    c: DistanceX(g0,g-1) = 0
FEATURE [PartDesign::Pocket] Pocket135  label="Screwheads Montage002"
  BaseFeature = -> Fillet045
  Length = 3
  Length2 = 100
  Profile = -> Sketch291
  Type = 0
FEATURE [Sketcher::SketchObject] Sketch292
  MapMode = 5
  Placement = pos=(0,0,2) rot=(0,0,1;0rad)
  Support = -> [Pocket135]
  sketch-geometry (3):
    g0: Circle [constr] CenterX=0 CenterY=15 CenterZ=0 NormalX=0 NormalY=0 NormalZ=1 AngleXU=0 Radius=35
    g1: Circle CenterX=-33.541 CenterY=25 CenterZ=0 NormalX=0 NormalY=0 NormalZ=1 AngleXU=0 Radius=1.6
    g2: Circle CenterX=-28.7228 CenterY=35 CenterZ=0 NormalX=0 NormalY=0 NormalZ=1 AngleXU=0 Radius=1.6
  constraints (9):
    c: Radius(g0) = 35
    c: PointOnObject(g1,g0)
    c: PointOnObject(g2,g0)
    c: Equal(g2,g1)
    c: Radius(g2) = 1.6
    c: DistanceY(g1,g2) = 10
    c: DistanceY(g-1,g0) = 15
    c: DistanceY(g0,g1) = 10
    c: DistanceX(g0,g-1) = 0
FEATURE [PartDesign::Pocket] Pocket136  label="Screwholes Montage002"
  BaseFeature = -> Pocket135
  Length = 3
  Length2 = 100
  Profile = -> Sketch292
  Type = 0
FEATURE [Sketcher::SketchObject] Sketch288
  MapMode = 5
  Placement = pos=(0,0,5) rot=(0,0,1;0rad)
  Support = -> [Pocket136]
  sketch-geometry (1):
    g0: Circle CenterX=0 CenterY=0 CenterZ=0 NormalX=0 NormalY=0 NormalZ=1 AngleXU=0 Radius=6.15
  constraints (2):
    c: Coincident(g0,g-1)
    c: Radius(g0) = 6.15
FEATURE [PartDesign::Pocket] Pocket137  label="Ball Bearing Flange"
  BaseFeature = -> Pocket136
  Length = 5
  Length2 = 100
  Profile = -> Sketch288
  Type = 0
FEATURE [Sketcher::SketchObject] Sketch293
  MapMode = 5
  Placement = pos=(0,0,0) rot=(1,0,0;3.14159rad)
  Support = -> [Pocket137]
  sketch-geometry (1):
    g0: Circle CenterX=0 CenterY=0 CenterZ=0 NormalX=0 NormalY=0 NormalZ=1 AngleXU=0 Radius=8.15
  constraints (2):
    c: Coincident(g0,g-1)
    c: Radius(g0) = 8.15
FEATURE [PartDesign::Pocket] Pocket138  label="Ball Bearing Pocket"
  BaseFeature = -> Pocket137
  Length = 4.5
  Length2 = 100
  Profile = -> Sketch293
  Type = 0
FEATURE [PartDesign::Fillet] Fillet047  label="Ball Bearing Pocket Bottom Fillet"
  Base = -> Pocket138 [Edge43]
  BaseFeature = -> Pocket138
  Radius = 1.8
FEATURE [PartDesign::Fillet] Fillet046  label="Smooth End Edge"
  Base = -> Fillet047 [Edge31]
  BaseFeature = -> Fillet047
  Radius = 0.4
FEATURE [PartDesign::Body] Body051  label="Limb_Ball_Bearing_Mount_long_v4"
  Group = -> [Sketch290,Pad094,Sketch289,SubtractivePipe002,Fillet045,Sketch291,Pocket135,Sketch292,Pocket136,Sketch288,Pocket137,Sketch293,Pocket138,Fillet047,Fillet046]
  Origin = -> Origin081
  Tip = -> Fillet046
FEATURE [App::Part] Part022  label="ball bearing moung"
  Group = -> [Body051]
  Origin = -> Origin080
  Placement = pos=(-144.1,22.7,27.05) rot=(0,0.707107,0.707107;3.14159rad)
FEATURE [Sketcher::SketchObject] Sketch191
  MapMode = 5
  Support = -> [XY_Plane029]
  sketch-geometry (1):
    g0: Circle CenterX=0 CenterY=0 CenterZ=0 NormalX=0 NormalY=0 NormalZ=1 AngleXU=0 Radius=2.75
  constraints (2):
    c: Coincident(g0,g-1)
    c: Radius(g0) = 2.75
FEATURE [Sketcher::SketchObject] Sketch304
  MapMode = 5
  Placement = pos=(0,0,0) rot=(1,0,0;1.5708rad)
  Support = -> [XZ_Plane082]
  sketch-geometry (1):
    g0: Circle CenterX=-1.55 CenterY=4 CenterZ=0 NormalX=0 NormalY=0 NormalZ=1 AngleXU=0 Radius=0.75
  constraints (3):
    c: Radius(g0) = 0.75
    c: DistanceY(g-1,g0) = 4
    c: DistanceX(g0,g-1) = 1.55
FEATURE [Sketcher::SketchObject] Sketch306
  MapMode = 5
  Placement = pos=(0,0,0) rot=(1,0,0;1.5708rad)
  Support = -> [XZ_Plane083]
  sketch-geometry (1):
    g0: Circle CenterX=0 CenterY=4 CenterZ=0 NormalX=0 NormalY=0 NormalZ=1 AngleXU=0 Radius=0.75
  constraints (3):
    c: PointOnObject(g0,g-2)
    c: Radius(g0) = 0.75
    c: DistanceY(g-1,g0) = 4
FEATURE [Sketcher::SketchObject] Sketch307
  MapMode = 5
  Placement = pos=(0,0,0) rot=(1,0,0;1.5708rad)
  Support = -> [XZ_Plane086]
  sketch-geometry (1):
    g0: Circle CenterX=1.55 CenterY=4 CenterZ=0 NormalX=0 NormalY=0 NormalZ=1 AngleXU=0 Radius=0.75
  constraints (3):
    c: Radius(g0) = 0.75
    c: DistanceY(g-1,g0) = 4
    c: DistanceX(g-1,g0) = 1.55
FEATURE [Sketcher::SketchObject] Sketch309
  MapMode = 5
  Support = -> [XY_Plane087]
  sketch-geometry (4):
    g0: LineSegment StartX=-10 StartY=20.15 StartZ=0 EndX=10 EndY=20.15 EndZ=0
    g1: LineSegment StartX=10 StartY=20.15 StartZ=0 EndX=10 EndY=-20.15 EndZ=0
    g2: LineSegment StartX=10 StartY=-20.15 StartZ=0 EndX=-10 EndY=-20.15 EndZ=0
    g3: LineSegment StartX=-10 StartY=-20.15 StartZ=0 EndX=-10 EndY=20.15 EndZ=0
  constraints (10):
    c: Coincident(g0,g1)
    c: Coincident(g1,g2)
    c: Coincident(g2,g3)
    c: Coincident(g3,g0)
    c: Horizontal(g2)
    c: Vertical(g3)
    c: DistanceX(g0,g0) = 20
    c: DistanceY(g1,g1) = 40.3
    c: Symmetric(g0,g1,g-1)
    c: Symmetric(g0,g0,g-2)
FEATURE [Sketcher::SketchObject] Sketch313
  MapMode = 5
  Support = -> [XY_Plane083]
  sketch-geometry (1):
    g0: Circle CenterX=0 CenterY=10.15 CenterZ=0 NormalX=0 NormalY=0 NormalZ=1 AngleXU=0 Radius=3
  constraints (3):
    c: PointOnObject(g0,g-2)
    c: DistanceY(g-1,g0) = 10.15
    c: Radius(g0) = 3
FEATURE [Sketcher::SketchObject] Sketch167
  MapMode = 5
  Support = -> [XY_Plane025]
  sketch-geometry (8):
    g0: LineSegment StartX=0 StartY=3.17543 StartZ=0 EndX=-2.75 EndY=1.58771 EndZ=0
    g1: LineSegment StartX=-2.75 StartY=1.58771 StartZ=0 EndX=-2.75 EndY=-1.58771 EndZ=0
    g2: LineSegment StartX=-2.75 StartY=-1.58771 StartZ=0 EndX=0 EndY=-3.17543 EndZ=0
    g3: LineSegment StartX=0 StartY=-3.17543 StartZ=0 EndX=2.75 EndY=-1.58771 EndZ=0
    g4: LineSegment StartX=2.75 StartY=-1.58771 StartZ=0 EndX=2.75 EndY=1.58771 EndZ=0
    g5: LineSegment StartX=2.75 StartY=1.58771 StartZ=0 EndX=0 EndY=3.17543 EndZ=0
    g6: Circle [constr] CenterX=0 CenterY=0 CenterZ=0 NormalX=0 NormalY=0 NormalZ=1 AngleXU=0 Radius=3.17543
    g7: Circle CenterX=0 CenterY=0 CenterZ=0 NormalX=0 NormalY=0 NormalZ=1 AngleXU=0 Radius=1.5
  constraints (18):
    c: Coincident(g0,g1)
    c: Coincident(g1,g2)
    c: Coincident(g2,g3)
    c: Coincident(g3,g4)
    c: Coincident(g4,g5)
    c: Coincident(g5,g0)
    c: Equal(g0, g1-g5) x5
    c: PointOnObject(g0,g6)
    c: PointOnObject(g1,g6)
    c: PointOnObject(g2,g6)
    c: PointOnObject(g3,g6)
    c: PointOnObject(g4,g6)
    c: PointOnObject(g5,g6)
    c: Coincident(g6,g-1)
    c: PointOnObject(g5,g-2)
    c: DistanceX(g0,g4) = 5.5
    c: Coincident(g7,g-1)
    c: Radius(g7) = 1.5
FEATURE [Sketcher::SketchObject] Sketch185
  MapMode = 5
  Support = -> [XY_Plane027]
  sketch-geometry (1):
    g0: Circle CenterX=0 CenterY=0 CenterZ=0 NormalX=0 NormalY=0 NormalZ=1 AngleXU=0 Radius=2.75
  constraints (2):
    c: Coincident(g0,g-1)
    c: Radius(g0) = 2.75
FEATURE [Sketcher::SketchObject] Sketch182
  MapMode = 5
  Support = -> [XY_Plane008]
  sketch-geometry (1):
    g0: Circle CenterX=0 CenterY=0 CenterZ=0 NormalX=0 NormalY=0 NormalZ=1 AngleXU=0 Radius=2.75
  constraints (2):
    c: Coincident(g0,g-1)
    c: Radius(g0) = 2.75
FEATURE [PartDesign::Pad] Pad039  label="M3 Nut Primitive016"
  Length = 1.2
  Length2 = 1.2
  Profile = -> Sketch167
  Type = 4
FEATURE [Sketcher::SketchObject] Sketch168
  ExternalGeometry = -> [Pad039]
  MapMode = 5
  Placement = pos=(0,0,0) rot=(0.57735,0.57735,0.57735;2.0944rad)
  Support = -> [YZ_Plane025]
  sketch-geometry (6):
    g0: LineSegment StartX=-2.67543 StartY=1.2 StartZ=0 EndX=-3.67543 EndY=1.2 EndZ=0
    g1: LineSegment StartX=-3.67543 StartY=1.2 StartZ=0 EndX=-3.67543 EndY=-1.2 EndZ=0
    g2: LineSegment StartX=-3.67543 StartY=-1.2 StartZ=0 EndX=-2.67543 EndY=-1.2 EndZ=0
    g3: LineSegment StartX=-2.67543 StartY=-1.2 StartZ=0 EndX=-3.17543 EndY=-1 EndZ=0
    g4: LineSegment StartX=-3.17543 StartY=-1 StartZ=0 EndX=-3.17543 EndY=1 EndZ=0
    g5: LineSegment StartX=-3.17543 StartY=1 StartZ=0 EndX=-2.67543 EndY=1.2 EndZ=0
  constraints (15):
    c: Horizontal(g0)
    c: Coincident(g0,g1)
    c: Coincident(g1,g2)
    c: Coincident(g2,g3)
    c: Coincident(g3,g4)
    c: Coincident(g4,g5)
    c: Coincident(g5,g0)
    c: Symmetric(g4,g3,g-1)
    c: Symmetric(g0,g2,g-1)
    c: Symmetric(g1,g0,g-1)
    c: DistanceX(g0,g4) = 0.5
    c: DistanceY(g3,g4) = 2
    c: DistanceY(g1,g0) = 2.4
    c: PointOnObject(g3,g-3)
    c: DistanceX(g4,g0) = 0.5
FEATURE [PartDesign::Pad] Pad048  label="M3x20 Head001"
  Length = 3
  Length2 = 100
  Profile = -> Sketch185
  Type = 0
FEATURE [Sketcher::SketchObject] Sketch186
  MapMode = 5
  Placement = pos=(0,0,3) rot=(0,0,1;0rad)
  Support = -> [Pad048]
  sketch-geometry (1):
    g0: Circle CenterX=0 CenterY=0 CenterZ=0 NormalX=0 NormalY=0 NormalZ=1 AngleXU=0 Radius=1.5
  constraints (2):
    c: Coincident(g0,g-1)
    c: Radius(g0) = 1.5
FEATURE [PartDesign::Pad] Pad049  label="M3x20 Thread001"
  BaseFeature = -> Pad048
  Length = 20
  Length2 = 100
  Profile = -> Sketch186
  Type = 0
FEATURE [Sketcher::SketchObject] Sketch187
  MapMode = 5
  Placement = pos=(0,0,0) rot=(1,0,0;3.14159rad)
  Support = -> [Pad049]
  sketch-geometry (7):
    g0: LineSegment StartX=1.275 StartY=0.736122 StartZ=0 EndX=0 EndY=1.47224 EndZ=0
    g1: LineSegment StartX=0 StartY=1.47224 StartZ=0 EndX=-1.275 EndY=0.736122 EndZ=0
    g2: LineSegment StartX=-1.275 StartY=0.736122 StartZ=0 EndX=-1.275 EndY=-0.736122 EndZ=0
    g3: LineSegment StartX=-1.275 StartY=-0.736122 StartZ=0 EndX=1.34766e-11 EndY=-1.47224 EndZ=0
    g4: LineSegment StartX=1.34766e-11 StartY=-1.47224 StartZ=0 EndX=1.275 EndY=-0.736122 EndZ=0
    g5: LineSegment StartX=1.275 StartY=-0.736122 StartZ=0 EndX=1.275 EndY=0.736122 EndZ=0
    g6: Circle [constr] CenterX=0 CenterY=0 CenterZ=0 NormalX=0 NormalY=0 NormalZ=1 AngleXU=0 Radius=1.47224
  constraints (16):
    c: Coincident(g0,g1)
    c: Coincident(g1,g2)
    c: Coincident(g2,g3)
    c: Coincident(g3,g4)
    c: Coincident(g4,g5)
    c: Coincident(g5,g0)
    c: Equal(g0, g1-g5) x5
    c: PointOnObject(g0,g6)
    c: PointOnObject(g1,g6)
    c: PointOnObject(g2,g6)
    c: PointOnObject(g3,g6)
    c: PointOnObject(g4,g6)
    c: PointOnObject(g5,g6)
    c: Coincident(g6,g-1)
    c: PointOnObject(g0,g-2)
    c: DistanceX(g1,g0) = 2.55
FEATURE [PartDesign::Pocket] Pocket110  label="M3x20 Wrench001"
  BaseFeature = -> Pad049
  Length = 1.3
  Length2 = 100
  Profile = -> Sketch187
  Type = 0
FEATURE [PartDesign::Chamfer] Chamfer031  label="M3x20 Smooth001"
  Base = -> Pocket110 [Face11,Edge2,Edge24,Edge3]
  BaseFeature = -> Pocket110
  Size = 0.2
FEATURE [PartDesign::Pad] Pad046  label="M3x20 Head"
  Length = 3
  Length2 = 100
  Profile = -> Sketch182
  Type = 0
FEATURE [Sketcher::SketchObject] Sketch183
  MapMode = 5
  Placement = pos=(0,0,3) rot=(0,0,1;0rad)
  Support = -> [Pad046]
  sketch-geometry (1):
    g0: Circle CenterX=0 CenterY=0 CenterZ=0 NormalX=0 NormalY=0 NormalZ=1 AngleXU=0 Radius=1.5
  constraints (2):
    c: Coincident(g0,g-1)
    c: Radius(g0) = 1.5
FEATURE [PartDesign::Pad] Pad047  label="M3x20 Thread"
  BaseFeature = -> Pad046
  Length = 20
  Length2 = 100
  Profile = -> Sketch183
  Type = 0
FEATURE [Sketcher::SketchObject] Sketch184
  MapMode = 5
  Placement = pos=(0,0,0) rot=(1,0,0;3.14159rad)
  Support = -> [Pad047]
  sketch-geometry (7):
    g0: LineSegment StartX=1.275 StartY=0.736122 StartZ=0 EndX=0 EndY=1.47224 EndZ=0
    g1: LineSegment StartX=0 StartY=1.47224 StartZ=0 EndX=-1.275 EndY=0.736122 EndZ=0
    g2: LineSegment StartX=-1.275 StartY=0.736122 StartZ=0 EndX=-1.275 EndY=-0.736122 EndZ=0
    g3: LineSegment StartX=-1.275 StartY=-0.736122 StartZ=0 EndX=1.34766e-11 EndY=-1.47224 EndZ=0
    g4: LineSegment StartX=1.34766e-11 StartY=-1.47224 StartZ=0 EndX=1.275 EndY=-0.736122 EndZ=0
    g5: LineSegment StartX=1.275 StartY=-0.736122 StartZ=0 EndX=1.275 EndY=0.736122 EndZ=0
    g6: Circle [constr] CenterX=0 CenterY=0 CenterZ=0 NormalX=0 NormalY=0 NormalZ=1 AngleXU=0 Radius=1.47224
  constraints (16):
    c: Coincident(g0,g1)
    c: Coincident(g1,g2)
    c: Coincident(g2,g3)
    c: Coincident(g3,g4)
    c: Coincident(g4,g5)
    c: Coincident(g5,g0)
    c: Equal(g0, g1-g5) x5
    c: PointOnObject(g0,g6)
    c: PointOnObject(g1,g6)
    c: PointOnObject(g2,g6)
    c: PointOnObject(g3,g6)
    c: PointOnObject(g4,g6)
    c: PointOnObject(g5,g6)
    c: Coincident(g6,g-1)
    c: PointOnObject(g0,g-2)
    c: DistanceX(g1,g0) = 2.55
FEATURE [PartDesign::Pocket] Pocket109  label="M3x20 Wrench"
  BaseFeature = -> Pad047
  Length = 1.3
  Length2 = 100
  Profile = -> Sketch184
  Type = 0
FEATURE [PartDesign::Chamfer] Chamfer033  label="M3x20 Smooth"
  Base = -> Pocket109 [Face11,Edge2,Edge24,Edge3]
  BaseFeature = -> Pocket109
  Size = 0.2
FEATURE [PartDesign::Groove] Groove018  label="M3 Nut Smooth017"
  Angle = 360
  Axis = (-2e-16,3e-16,1)
  Base = (0,0,0)
  BaseFeature = -> Pad039
  Profile = -> Sketch168
  ReferenceAxis = -> Sketch168 [V_Axis]
  Reversed = true
FEATURE [PartDesign::Chamfer] Chamfer030  label="M3 Nut Smooth Hole014"
  Base = -> Groove018 [Edge24,Edge23]
  BaseFeature = -> Groove018
  Size = 0.2
FEATURE [PartDesign::Pad] Pad099  label="Baseblock002"
  Length = 26.6
  Length2 = 100
  Profile = -> Sketch309
  Type = 0
FEATURE [Sketcher::SketchObject] Sketch299
  MapMode = 5
  Placement = pos=(0,0,26.6) rot=(0,0,1;0rad)
  Support = -> [Pad099]
  sketch-geometry (4):
    g0: LineSegment StartX=-10 StartY=-26.8 StartZ=0 EndX=10 EndY=-26.8 EndZ=0
    g1: LineSegment StartX=10 StartY=-26.8 StartZ=0 EndX=10 EndY=26.8 EndZ=0
    g2: LineSegment StartX=10 StartY=26.8 StartZ=0 EndX=-10 EndY=26.8 EndZ=0
    g3: LineSegment StartX=-10 StartY=26.8 StartZ=0 EndX=-10 EndY=-26.8 EndZ=0
  constraints (10):
    c: Coincident(g0,g1)
    c: Coincident(g1,g2)
    c: Coincident(g2,g3)
    c: Coincident(g3,g0)
    c: Horizontal(g0)
    c: Vertical(g3)
    c: Symmetric(g1,g2,g-2)
    c: Symmetric(g1,g0,g-1)
    c: DistanceX(g2,g2) = 20
    c: DistanceY(g1,g1) = 53.6
FEATURE [PartDesign::Pad] Pad052  label="M3x20 Head003"
  Length = 3
  Length2 = 100
  Profile = -> Sketch191
  Type = 0
FEATURE [Sketcher::SketchObject] Sketch192
  MapMode = 5
  Placement = pos=(0,0,3) rot=(0,0,1;0rad)
  Support = -> [Pad052]
  sketch-geometry (1):
    g0: Circle CenterX=0 CenterY=0 CenterZ=0 NormalX=0 NormalY=0 NormalZ=1 AngleXU=0 Radius=1.5
  constraints (2):
    c: Coincident(g0,g-1)
    c: Radius(g0) = 1.5
FEATURE [PartDesign::Pad] Pad053  label="M3x20 Thread003"
  BaseFeature = -> Pad052
  Length = 20
  Length2 = 100
  Profile = -> Sketch192
  Type = 0
FEATURE [Sketcher::SketchObject] Sketch193
  MapMode = 5
  Placement = pos=(0,0,0) rot=(1,0,0;3.14159rad)
  Support = -> [Pad053]
  sketch-geometry (7):
    g0: LineSegment StartX=1.275 StartY=0.736122 StartZ=0 EndX=0 EndY=1.47224 EndZ=0
    g1: LineSegment StartX=0 StartY=1.47224 StartZ=0 EndX=-1.275 EndY=0.736122 EndZ=0
    g2: LineSegment StartX=-1.275 StartY=0.736122 StartZ=0 EndX=-1.275 EndY=-0.736122 EndZ=0
    g3: LineSegment StartX=-1.275 StartY=-0.736122 StartZ=0 EndX=1.34766e-11 EndY=-1.47224 EndZ=0
    g4: LineSegment StartX=1.34766e-11 StartY=-1.47224 StartZ=0 EndX=1.275 EndY=-0.736122 EndZ=0
    g5: LineSegment StartX=1.275 StartY=-0.736122 StartZ=0 EndX=1.275 EndY=0.736122 EndZ=0
    g6: Circle [constr] CenterX=0 CenterY=0 CenterZ=0 NormalX=0 NormalY=0 NormalZ=1 AngleXU=0 Radius=1.47224
  constraints (16):
    c: Coincident(g0,g1)
    c: Coincident(g1,g2)
    c: Coincident(g2,g3)
    c: Coincident(g3,g4)
    c: Coincident(g4,g5)
    c: Coincident(g5,g0)
    c: Equal(g0, g1-g5) x5
    c: PointOnObject(g0,g6)
    c: PointOnObject(g1,g6)
    c: PointOnObject(g2,g6)
    c: PointOnObject(g3,g6)
    c: PointOnObject(g4,g6)
    c: PointOnObject(g5,g6)
    c: Coincident(g6,g-1)
    c: PointOnObject(g0,g-2)
    c: DistanceX(g1,g0) = 2.55
FEATURE [PartDesign::Pocket] Pocket144  label="M3x20 Wrench003"
  BaseFeature = -> Pad053
  Length = 1.3
  Length2 = 100
  Profile = -> Sketch193
  Type = 0
FEATURE [PartDesign::Chamfer] Chamfer034  label="M3x20 Smooth003"
  Base = -> Pocket144 [Face11,Edge2,Edge24,Edge3]
  BaseFeature = -> Pocket144
  Size = 0.2
FEATURE [PartDesign::Pad] Pad103
  Length = 10
  Length2 = 100
  Placement = pos=(0,0,0) rot=(1,0,0;1.5708rad)
  Profile = -> Sketch306
  Reversed = true
  Type = 0
FEATURE [Sketcher::SketchObject] Sketch188
  MapMode = 5
  Support = -> [XY_Plane028]
  sketch-geometry (1):
    g0: Circle CenterX=0 CenterY=0 CenterZ=0 NormalX=0 NormalY=0 NormalZ=1 AngleXU=0 Radius=2.75
  constraints (2):
    c: Coincident(g0,g-1)
    c: Radius(g0) = 2.75
FEATURE [PartDesign::Pad] Pad050  label="M3x20 Head002"
  Length = 3
  Length2 = 100
  Profile = -> Sketch188
  Type = 0
FEATURE [Sketcher::SketchObject] Sketch189
  MapMode = 5
  Placement = pos=(0,0,3) rot=(0,0,1;0rad)
  Support = -> [Pad050]
  sketch-geometry (1):
    g0: Circle CenterX=0 CenterY=0 CenterZ=0 NormalX=0 NormalY=0 NormalZ=1 AngleXU=0 Radius=1.5
  constraints (2):
    c: Coincident(g0,g-1)
    c: Radius(g0) = 1.5
FEATURE [PartDesign::Pad] Pad051  label="M3x20 Thread002"
  BaseFeature = -> Pad050
  Length = 20
  Length2 = 100
  Profile = -> Sketch189
  Type = 0
FEATURE [Sketcher::SketchObject] Sketch190
  MapMode = 5
  Placement = pos=(0,0,0) rot=(1,0,0;3.14159rad)
  Support = -> [Pad051]
  sketch-geometry (7):
    g0: LineSegment StartX=1.275 StartY=0.736122 StartZ=0 EndX=0 EndY=1.47224 EndZ=0
    g1: LineSegment StartX=0 StartY=1.47224 StartZ=0 EndX=-1.275 EndY=0.736122 EndZ=0
    g2: LineSegment StartX=-1.275 StartY=0.736122 StartZ=0 EndX=-1.275 EndY=-0.736122 EndZ=0
    g3: LineSegment StartX=-1.275 StartY=-0.736122 StartZ=0 EndX=1.34766e-11 EndY=-1.47224 EndZ=0
    g4: LineSegment StartX=1.34766e-11 StartY=-1.47224 StartZ=0 EndX=1.275 EndY=-0.736122 EndZ=0
    g5: LineSegment StartX=1.275 StartY=-0.736122 StartZ=0 EndX=1.275 EndY=0.736122 EndZ=0
    g6: Circle [constr] CenterX=0 CenterY=0 CenterZ=0 NormalX=0 NormalY=0 NormalZ=1 AngleXU=0 Radius=1.47224
  constraints (16):
    c: Coincident(g0,g1)
    c: Coincident(g1,g2)
    c: Coincident(g2,g3)
    c: Coincident(g3,g4)
    c: Coincident(g4,g5)
    c: Coincident(g5,g0)
    c: Equal(g0, g1-g5) x5
    c: PointOnObject(g0,g6)
    c: PointOnObject(g1,g6)
    c: PointOnObject(g2,g6)
    c: PointOnObject(g3,g6)
    c: PointOnObject(g4,g6)
    c: PointOnObject(g5,g6)
    c: Coincident(g6,g-1)
    c: PointOnObject(g0,g-2)
    c: DistanceX(g1,g0) = 2.55
FEATURE [PartDesign::Pocket] Pocket111  label="M3x20 Wrench002"
  BaseFeature = -> Pad051
  Length = 1.3
  Length2 = 100
  Profile = -> Sketch190
  Type = 0
FEATURE [PartDesign::Chamfer] Chamfer032  label="M3x20 Smooth002"
  Base = -> Pocket111 [Face11,Edge2,Edge24,Edge3]
  BaseFeature = -> Pocket111
  Size = 0.2
FEATURE [PartDesign::Pad] Pad105
  Length = 5
  Length2 = 100
  Profile = -> Sketch313
  Type = 0
FEATURE [Sketcher::SketchObject] Sketch305
  ExternalGeometry = -> [Pad105]
  MapMode = 5
  Placement = pos=(0,0,5) rot=(0,0,1;0rad)
  Support = -> [Pad105]
  sketch-geometry (1):
    g0: Circle CenterX=0 CenterY=10.15 CenterZ=0 NormalX=0 NormalY=0 NormalZ=1 AngleXU=0 Radius=1.5
  constraints (2):
    c: Coincident(g0,g-3)
    c: Radius(g0) = 1.5
FEATURE [PartDesign::Pad] Pad109
  Length = 10
  Length2 = 100
  Placement = pos=(0,0,0) rot=(1,0,0;1.5708rad)
  Profile = -> Sketch307
  Reversed = true
  Type = 0
FEATURE [PartDesign::Pad] Pad110
  Length = 10
  Length2 = 100
  Placement = pos=(0,0,0) rot=(1,0,0;1.5708rad)
  Profile = -> Sketch304
  Reversed = true
  Type = 0
FEATURE [PartDesign::Pad] Pad112
  BaseFeature = -> Pad099
  Length = 2.5
  Length2 = 100
  Profile = -> Sketch299
  Type = 0
FEATURE [Sketcher::SketchObject] Sketch300
  MapMode = 5
  Placement = pos=(0,0,29.1) rot=(0,0,1;0rad)
  Support = -> [Pad112]
  sketch-geometry (4):
    g0: LineSegment StartX=-10 StartY=-20.15 StartZ=0 EndX=10 EndY=-20.15 EndZ=0
    g1: LineSegment StartX=10 StartY=-20.15 StartZ=0 EndX=10 EndY=20.15 EndZ=0
    g2: LineSegment StartX=10 StartY=20.15 StartZ=0 EndX=-10 EndY=20.15 EndZ=0
    g3: LineSegment StartX=-10 StartY=20.15 StartZ=0 EndX=-10 EndY=-20.15 EndZ=0
  constraints (10):
    c: Coincident(g0,g1)
    c: Coincident(g1,g2)
    c: Coincident(g2,g3)
    c: Coincident(g3,g0)
    c: Horizontal(g0)
    c: Vertical(g3)
    c: Symmetric(g1,g2,g-2)
    c: Symmetric(g1,g0,g-1)
    c: DistanceX(g2,g2) = 20
    c: DistanceY(g1,g1) = 40.3
FEATURE [PartDesign::Pad] Pad101
  BaseFeature = -> Pad112
  Length = 6
  Length2 = 100
  Profile = -> Sketch300
  Type = 0
FEATURE [Sketcher::SketchObject] Sketch303
  ExternalGeometry = -> [Pad101]
  MapMode = 5
  Placement = pos=(0,0,35.1) rot=(0,0,1;0rad)
  Support = -> [Pad101]
  sketch-geometry (7):
    g0: ArcOfCircle CenterX=-3e-16 CenterY=10.15 CenterZ=0 NormalX=0 NormalY=0 NormalZ=1 AngleXU=0 Radius=9.5 StartAngle=5.9573 EndAngle=9.75066
    g1: LineSegment StartX=-9 StartY=7.10862 StartZ=0 EndX=-9 EndY=-14.15 EndZ=0
    g2: LineSegment StartX=-9 StartY=-14.15 StartZ=0 EndX=-5 EndY=-14.15 EndZ=0
    g3: LineSegment StartX=5 StartY=-14.15 StartZ=0 EndX=9 EndY=-14.15 EndZ=0
    g4: LineSegment StartX=9 StartY=-14.15 StartZ=0 EndX=9 EndY=7.10862 EndZ=0
    g5: ArcOfCircle CenterX=-3e-16 CenterY=-10.4 CenterZ=0 NormalX=0 NormalY=0 NormalZ=1 AngleXU=0 Radius=6.25 StartAngle=3.78509 EndAngle=5.63968
    g6: LineSegment [constr] StartX=0 StartY=-20.15 StartZ=0 EndX=0 EndY=-16.65 EndZ=0
  constraints (22):
    c: Symmetric(g0,g0,g-2)
    c: Coincident(g1,g0)
    c: Vertical(g1)
    c: Coincident(g2,g1)
    c: Horizontal(g2)
    c: Horizontal(g3)
    c: Coincident(g4,g3)
    c: Coincident(g4,g0)
    c: Vertical(g4)
    c: Symmetric(g2,g3,g-2)
    c: Coincident(g5,g2)
    c: Coincident(g5,g3)
    c: DistanceY(g-3,g3) = 6
    c: DistanceY(g0,g-4) = 10
    c: Radius(g0) = 9.5
    c: DistanceX(g0,g0) = 18
    c: PointOnObject(g6,g-3)
    c: PointOnObject(g6,g5)
    c: Vertical(g6)
    c: DistanceY(g6,g6) = 3.5
    c: DistanceX(g2,g3) = 10
    c: PointOnObject(g6,g-2)
FEATURE [PartDesign::Pad] Pad102
  BaseFeature = -> Pad101
  Length = 2.5
  Length2 = 100
  Profile = -> Sketch303
  Type = 0
FEATURE [Sketcher::SketchObject] Sketch296
  ExternalGeometry = -> [Pad102]
  MapMode = 5
  Placement = pos=(0,0,37.6) rot=(0,0,1;0rad)
  Support = -> [Pad102]
  sketch-geometry (1):
    g0: Circle CenterX=-3e-16 CenterY=10.15 CenterZ=0 NormalX=0 NormalY=0 NormalZ=1 AngleXU=0 Radius=6.5
  constraints (2):
    c: Coincident(g0,g-3)
    c: Radius(g0) = 6.5
FEATURE [PartDesign::Pad] Pad104
  BaseFeature = -> Pad102
  Length = 1
  Length2 = 100
  Profile = -> Sketch296
  Type = 0
FEATURE [Sketcher::SketchObject] Sketch295
  ExternalGeometry = -> [Pad104]
  MapMode = 5
  Placement = pos=(0,0,38.6) rot=(0,0,1;0rad)
  Support = -> [Pad104]
  sketch-geometry (1):
    g0: Circle CenterX=0 CenterY=10.15 CenterZ=0 NormalX=0 NormalY=0 NormalZ=1 AngleXU=0 Radius=5.5
  constraints (2):
    c: Coincident(g0,g-3)
    c: Radius(g0) = 5.5
FEATURE [PartDesign::Pad] Pad108
  BaseFeature = -> Pad104
  Length = 0.5
  Length2 = 100
  Profile = -> Sketch295
  Type = 0
FEATURE [Sketcher::SketchObject] Sketch311
  ExternalGeometry = -> [Pad108]
  MapMode = 5
  Placement = pos=(0,0,39.1) rot=(0,0,1;0rad)
  Support = -> [Pad108]
  sketch-geometry (1):
    g0: Circle CenterX=0 CenterY=10.15 CenterZ=0 NormalX=0 NormalY=0 NormalZ=1 AngleXU=0 Radius=3
  constraints (2):
    c: Coincident(g0,g-3)
    c: Radius(g0) = 3
FEATURE [PartDesign::Pad] Pad107
  BaseFeature = -> Pad108
  Length = 4
  Length2 = 100
  Profile = -> Sketch311
  Type = 0
FEATURE [Sketcher::SketchObject] Sketch312
  ExternalGeometry = -> [Pad107]
  MapMode = 5
  Placement = pos=(0,0,43.1) rot=(0,0,1;0rad)
  Support = -> [Pad107]
  sketch-geometry (1):
    g0: Circle CenterX=0 CenterY=10.15 CenterZ=0 NormalX=0 NormalY=0 NormalZ=1 AngleXU=0 Radius=1.5
  constraints (2):
    c: Coincident(g0,g-3)
    c: Radius(g0) = 1.5
FEATURE [PartDesign::Pocket] Pocket148
  BaseFeature = -> Pad107
  Length = 5
  Length2 = 100
  Profile = -> Sketch312
  Type = 0
FEATURE [Sketcher::SketchObject] Sketch297
  MapMode = 5
  Placement = pos=(0,0,29.1) rot=(0,0,1;0rad)
  Support = -> [Pocket148]
  sketch-geometry (4):
    g0: Circle CenterX=-4.91157 CenterY=25.3 CenterZ=0 NormalX=0 NormalY=0 NormalZ=1 AngleXU=0 Radius=2.25
    g1: Circle CenterX=4.91157 CenterY=25.3 CenterZ=0 NormalX=0 NormalY=0 NormalZ=1 AngleXU=0 Radius=2.25
    g2: Circle CenterX=-4.91157 CenterY=-25.3 CenterZ=0 NormalX=0 NormalY=0 NormalZ=1 AngleXU=0 Radius=2.25
    g3: Circle CenterX=4.91157 CenterY=-25.3 CenterZ=0 NormalX=0 NormalY=0 NormalZ=1 AngleXU=0 Radius=2.25
  constraints (8):
    c: Equal(g3,g2)
    c: Equal(g2,g1)
    c: Equal(g1,g0)
    c: Radius(g1) = 2.25
    c: Symmetric(g1,g0,g-2)
    c: Symmetric(g3,g2,g-2)
    c: Symmetric(g3,g1,g-1)
    c: DistanceY(g3,g1) = 50.6
FEATURE [PartDesign::Pocket] Pocket145
  BaseFeature = -> Pocket148
  Length = 5
  Length2 = 100
  Profile = -> Sketch297
  Type = 0
FEATURE [Sketcher::SketchObject] Sketch308
  MapMode = 5
  Placement = pos=(0,0,29.1) rot=(0,0,1;0rad)
  Support = -> [Pocket145]
  sketch-geometry (8):
    g0: LineSegment StartX=-0.5 StartY=26.8 StartZ=0 EndX=0.5 EndY=26.8 EndZ=0
    g1: LineSegment StartX=0.5 StartY=26.8 StartZ=0 EndX=0.5 EndY=20.15 EndZ=0
    g2: LineSegment StartX=0.5 StartY=20.15 StartZ=0 EndX=-0.5 EndY=20.15 EndZ=0
    g3: LineSegment StartX=-0.5 StartY=20.15 StartZ=0 EndX=-0.5 EndY=26.8 EndZ=0
    g4: LineSegment StartX=-0.5 StartY=-20.15 StartZ=0 EndX=0.5 EndY=-20.15 EndZ=0
    g5: LineSegment StartX=0.5 StartY=-20.15 StartZ=0 EndX=0.5 EndY=-26.8 EndZ=0
    g6: LineSegment StartX=0.5 StartY=-26.8 StartZ=0 EndX=-0.5 EndY=-26.8 EndZ=0
    g7: LineSegment StartX=-0.5 StartY=-26.8 StartZ=0 EndX=-0.5 EndY=-20.15 EndZ=0
  constraints (20):
    c: Coincident(g0,g1)
    c: Coincident(g1,g2)
    c: Coincident(g2,g3)
    c: Coincident(g3,g0)
    c: Horizontal(g2)
    c: Vertical(g1)
    c: Vertical(g3)
    c: Coincident(g4,g5)
    c: Coincident(g5,g6)
    c: Coincident(g6,g7)
    c: Coincident(g7,g4)
    c: Horizontal(g6)
    c: Vertical(g7)
    c: Symmetric(g4,g4,g-2)
    c: Symmetric(g0,g0,g-2)
    c: Symmetric(g0,g5,g-1)
    c: DistanceY(g5,g0) = 53.6
    c: DistanceY(g4,g1) = 40.3
    c: DistanceX(g0,g0) = 1
    c: Symmetric(g4,g1,g-1)
FEATURE [PartDesign::Pad] Pad111
  BaseFeature = -> Pocket145
  Length = 2
  Length2 = 100
  Profile = -> Sketch308
  Type = 0
FEATURE [Sketcher::SketchObject] Sketch310
  ExternalGeometry = -> [Pad111]
  MapMode = 5
  Placement = pos=(0.5,0,0) rot=(0.57735,0.57735,0.57735;2.0944rad)
  Support = -> [Pad111]
  sketch-geometry (6):
    g0: LineSegment StartX=-26.8 StartY=29.1 StartZ=0 EndX=-26.8 EndY=31.1 EndZ=0
    g1: LineSegment StartX=-26.8 StartY=31.1 StartZ=0 EndX=-20.15 EndY=31.1 EndZ=0
    g2: LineSegment StartX=-20.15 StartY=31.1 StartZ=0 EndX=-26.8 EndY=29.1 EndZ=0
    g3: LineSegment StartX=20.15 StartY=31.1 StartZ=0 EndX=26.8 EndY=31.1 EndZ=0
    g4: LineSegment StartX=26.8 StartY=31.1 StartZ=0 EndX=26.8 EndY=29.1 EndZ=0
    g5: LineSegment StartX=26.8 StartY=29.1 StartZ=0 EndX=20.15 EndY=31.1 EndZ=0
  constraints (14):
    c: Vertical(g0)
    c: Coincident(g0,g1)
    c: Horizontal(g1)
    c: Coincident(g1,g2)
    c: Coincident(g2,g0)
    c: Coincident(g3,g4)
    c: Coincident(g4,g5)
    c: Coincident(g5,g3)
    c: Symmetric(g0,g4,g-2)
    c: Symmetric(g3,g0,g-2)
    c: Symmetric(g1,g3,g-2)
    c: DistanceX(g0,g3) = 53.6
    c: DistanceY(g4,g4) = 2
    c: Coincident(g3,g-3)
FEATURE [PartDesign::Pocket] Pocket147
  BaseFeature = -> Pad111
  Length = 1
  Length2 = 100
  Profile = -> Sketch310
  Type = 0
FEATURE [PartDesign::Pocket] Pocket149
  BaseFeature = -> Pad105
  Length = 4
  Length2 = 100
  Profile = -> Sketch305
  Type = 0
FEATURE [PartDesign::Chamfer] Chamfer041
  Base = -> Pocket149 [Edge3]
  BaseFeature = -> Pocket149
  Size = 0.25
FEATURE [PartDesign::Fillet] Fillet049
  Base = -> Pocket147 [Edge26,Edge27,Edge72,Edge63,Edge70,Edge78,Edge51,Edge49,Edge71,Edge50,Edge79,Edge86,Edge30,Edge21,Edge4,Edge29,Edge105,Edge107,Edge109,Edge111,Edge113,Edge114,Edge123]
  BaseFeature = -> Pocket147
  Radius = 0.4
FEATURE [Sketcher::SketchObject] Sketch302
  MapMode = 5
  Placement = pos=(0,20.15,0) rot=(0,0.707107,0.707107;3.14159rad)
  Support = -> [Fillet049]
  sketch-geometry (4):
    g0: LineSegment StartX=-3.25 StartY=2 StartZ=0 EndX=3.25 EndY=2 EndZ=0
    g1: LineSegment StartX=3.25 StartY=2 StartZ=0 EndX=3.25 EndY=6 EndZ=0
    g2: LineSegment StartX=3.25 StartY=6 StartZ=0 EndX=-3.25 EndY=6 EndZ=0
    g3: LineSegment StartX=-3.25 StartY=6 StartZ=0 EndX=-3.25 EndY=2 EndZ=0
  constraints (11):
    c: Coincident(g0,g1)
    c: Coincident(g1,g2)
    c: Coincident(g2,g3)
    c: Coincident(g3,g0)
    c: Horizontal(g0)
    c: Vertical(g1)
    c: Vertical(g3)
    c: DistanceY(g-1,g0) = 2
    c: DistanceY(g1,g1) = 4
    c: Symmetric(g2,g1,g-2)
    c: DistanceX(g2,g2) = 6.5
FEATURE [PartDesign::Pad] Pad113
  BaseFeature = -> Fillet049
  Length = 1
  Length2 = 100
  Profile = -> Sketch302
  Type = 0
FEATURE [Sketcher::SketchObject] Sketch301
  MapMode = 5
  Placement = pos=(0,21.15,0) rot=(0,0.707107,0.707107;3.14159rad)
  Support = -> [Pad113]
  sketch-geometry (4):
    g0: LineSegment StartX=-2.75 StartY=5.5 StartZ=0 EndX=2.75 EndY=5.5 EndZ=0
    g1: LineSegment StartX=2.75 StartY=5.5 StartZ=0 EndX=2.75 EndY=2.5 EndZ=0
    g2: LineSegment StartX=2.75 StartY=2.5 StartZ=0 EndX=-2.75 EndY=2.5 EndZ=0
    g3: LineSegment StartX=-2.75 StartY=2.5 StartZ=0 EndX=-2.75 EndY=5.5 EndZ=0
  constraints (11):
    c: Coincident(g0,g1)
    c: Coincident(g1,g2)
    c: Coincident(g2,g3)
    c: Coincident(g3,g0)
    c: Horizontal(g0)
    c: Vertical(g1)
    c: Vertical(g3)
    c: Symmetric(g1,g2,g-2)
    c: DistanceY(g1,g0) = 3
    c: DistanceY(g-1,g1) = 2.5
    c: DistanceX(g0,g0) = 5.5
FEATURE [PartDesign::Pad] Pad100
  BaseFeature = -> Pad113
  Length = 4
  Length2 = 100
  Profile = -> Sketch301
  Type = 0
FEATURE [Sketcher::SketchObject] Sketch298
  MapMode = 5
  Placement = pos=(0,0,0) rot=(1,0,0;3.14159rad)
  Support = -> [Pad100]
  sketch-geometry (4):
    g0: LineSegment StartX=-10 StartY=-20.15 StartZ=0 EndX=10 EndY=-20.15 EndZ=0
    g1: LineSegment StartX=10 StartY=-20.15 StartZ=0 EndX=10 EndY=20.15 EndZ=0
    g2: LineSegment StartX=10 StartY=20.15 StartZ=0 EndX=-10 EndY=20.15 EndZ=0
    g3: LineSegment StartX=-10 StartY=20.15 StartZ=0 EndX=-10 EndY=-20.15 EndZ=0
  constraints (10):
    c: Coincident(g0,g1)
    c: Coincident(g1,g2)
    c: Coincident(g2,g3)
    c: Coincident(g3,g0)
    c: Horizontal(g0)
    c: Vertical(g1)
    c: Symmetric(g2,g1,g-2)
    c: Symmetric(g0,g2,g-1)
    c: DistanceX(g2,g2) = 20
    c: DistanceY(g1,g1) = 40.3
FEATURE [PartDesign::Pad] Pad106
  BaseFeature = -> Pad100
  Length = 2
  Length2 = 100
  Profile = -> Sketch298
  Type = 0
FEATURE [PartDesign::Chamfer] Chamfer040
  Base = -> Pad106 [Face7]
  BaseFeature = -> Pad106
  Size = 1.5
FEATURE [PartDesign::Fillet] Fillet048
  Base = -> Chamfer040 [Edge1,Edge7,Edge18,Edge4,Face12]
  BaseFeature = -> Chamfer040
  Radius = 0.4
FEATURE [Sketcher::SketchObject] Sketch294
  ExternalGeometry = -> [Fillet048]
  MapMode = 5
  Placement = pos=(0,0,43.1) rot=(0,0,1;0rad)
  Support = -> [Fillet048]
  sketch-geometry (1):
    g0: Circle CenterX=0 CenterY=10.15 CenterZ=0 NormalX=0 NormalY=0 NormalZ=1 AngleXU=0 Radius=3
  constraints (2):
    c: Coincident(g0,g-3)
    c: Radius(g0) = 3
FEATURE [PartDesign::Pocket] Pocket146
  BaseFeature = -> Fillet048
  Length = 5
  Length2 = 100
  Profile = -> Sketch294
  Type = 0
FEATURE [Sketcher::SketchObject] Sketch116
  MapMode = 5
  Support = -> [XY_Plane090]
  sketch-geometry (9):
    g0: LineSegment StartX=-2.8e-15 StartY=0 StartZ=0 EndX=56.5 EndY=0 EndZ=0
    g1: LineSegment StartX=56.5 StartY=0 StartZ=0 EndX=56.5 EndY=25 EndZ=0
    g2: LineSegment StartX=51.5 StartY=30 StartZ=0 EndX=-80 EndY=30 EndZ=0
    g3: ArcOfCircle CenterX=-80 CenterY=15 CenterZ=0 NormalX=0 NormalY=0 NormalZ=1 AngleXU=0 Radius=15 StartAngle=1.5708 EndAngle=5.50197
    g4: ArcOfCircle CenterX=-50 CenterY=-14.75 CenterZ=0 NormalX=0 NormalY=0 NormalZ=1 AngleXU=0 Radius=27.25 StartAngle=1.5708 EndAngle=2.36038
    g5: ArcOfCircle CenterX=-30 CenterY=-14.75 CenterZ=0 NormalX=0 NormalY=0 NormalZ=1 AngleXU=0 Radius=27.25 StartAngle=0.781214 EndAngle=1.5708
    g6: ArcOfCircle CenterX=0 CenterY=15 CenterZ=0 NormalX=0 NormalY=0 NormalZ=1 AngleXU=0 Radius=15 StartAngle=3.92281 EndAngle=4.71239
    g7: LineSegment StartX=-50 StartY=12.5 StartZ=0 EndX=-30 EndY=12.5 EndZ=0
    g8: ArcOfCircle CenterX=51.5 CenterY=25 CenterZ=0 NormalX=0 NormalY=0 NormalZ=1 AngleXU=0 Radius=5 StartAngle=3e-16 EndAngle=1.5708
  constraints (23):
    c: Coincident(g0,g1)
    c: Horizontal(g0)
    c: Horizontal(g2)
    c: Vertical(g1)
    c: DistanceX(g0,g0) = 56.5
    c: Horizontal(g7)
    c: Radius(g3) = 15
    c: Tangent(g7,g5) = 1.5708
    c: Tangent(g4,g3) = 1.5708
    c: Tangent(g3,g2) = -1.5708
    c: Tangent(g7,g4) = 1.5708
    c: Tangent(g6,g5) = 1.5708
    c: Tangent(g6,g0) = -1.5708
    c: Equal(g3,g6)
    c: Equal(g4,g5)
    c: DistanceY(g0,g5) = 12.5
    c: DistanceX(g2,g0) = 80
    c: DistanceX(g4,g5) = 20
    c: Tangent(g3,g-1)
    c: Tangent(g2,g8) = -1.5708
    c: Tangent(g1,g8) = -1.5708
    c: Radius(g8) = 5
    c: Coincident(g0,g-1)
FEATURE [PartDesign::Pad] Pad021  label="Baseplate003"
  Length = 20
  Length2 = 100
  Profile = -> Sketch116
  Type = 0
FEATURE [Sketcher::SketchObject] Sketch117
  ExternalGeometry = -> [Pad021]
  MapMode = 5
  Placement = pos=(0,0,20) rot=(0,0,1;0rad)
  Support = -> [Pad021]
  sketch-geometry (18):
    g0: LineSegment StartX=-87.0711 StartY=22.0711 StartZ=0 EndX=-72.9287 EndY=7.92875 EndZ=0
    g1: LineSegment StartX=-50 StartY=17.1099 StartZ=0 EndX=-30 EndY=17.1099 EndZ=0
    g2: LineSegment StartX=-30 StartY=17.1099 StartZ=0 EndX=-30 EndY=25 EndZ=0
    g3: LineSegment StartX=-30 StartY=25 StartZ=0 EndX=-50 EndY=25 EndZ=0
    g4: LineSegment StartX=-50 StartY=25 StartZ=0 EndX=-50 EndY=17.1099 EndZ=0
    g5: LineSegment StartX=-55 StartY=25 StartZ=0 EndX=-55 EndY=17.1099 EndZ=0
    g6: LineSegment StartX=-55 StartY=25 StartZ=0 EndX=-80 EndY=25 EndZ=0
    g7: LineSegment StartX=-25 StartY=25 StartZ=0 EndX=-25 EndY=17.1099 EndZ=0
    g8: ArcOfCircle CenterX=-80 CenterY=15 CenterZ=0 NormalX=0 NormalY=0 NormalZ=1 AngleXU=0 Radius=10 StartAngle=1.5708 EndAngle=2.35619
    g9: ArcOfCircle CenterX=-50 CenterY=-14.75 CenterZ=0 NormalX=0 NormalY=0 NormalZ=1 AngleXU=0 Radius=32.2499 StartAngle=1.72646 EndAngle=2.36168
    g10: ArcOfCircle CenterX=-30 CenterY=-14.75 CenterZ=0 NormalX=0 NormalY=0 NormalZ=1 AngleXU=0 Radius=32.2499 StartAngle=0.781214 EndAngle=1.41513
    g11: ArcOfCircle CenterX=0 CenterY=15 CenterZ=0 NormalX=0 NormalY=0 NormalZ=1 AngleXU=0 Radius=10.0001 StartAngle=3.92281 EndAngle=4.1888
    g12: LineSegment StartX=-25 StartY=25 StartZ=0 EndX=-5 EndY=25 EndZ=0
    g13: LineSegment StartX=-5 StartY=25 StartZ=0 EndX=-5 EndY=6.33958 EndZ=0
    g14: LineSegment StartX=8 StartY=25 StartZ=0 EndX=48.5 EndY=25 EndZ=0
    g15: LineSegment StartX=48.5 StartY=25 StartZ=0 EndX=48.5 EndY=5 EndZ=0
    g16: LineSegment StartX=48.5 StartY=5 StartZ=0 EndX=8 EndY=5 EndZ=0
    g17: LineSegment StartX=8 StartY=5 StartZ=0 EndX=8 EndY=25 EndZ=0
  constraints (52):
    c: Coincident(g1,g2)
    c: Coincident(g2,g3)
    c: Coincident(g3,g4)
    c: Coincident(g4,g1)
    c: Horizontal(g1)
    c: Horizontal(g3)
    c: Vertical(g2)
    c: Vertical(g4)
    c: Coincident(g6,g5)
    c: Horizontal(g6)
    c: Vertical(g7)
    c: Vertical(g5)
    c: Coincident(g8,g0)
    c: Coincident(g9,g5)
    c: Coincident(g10,g7)
    c: Coincident(g12,g7)
    c: Horizontal(g12)
    c: Tangent(g8,g6) = -1.5708
    c: Horizontal(g5,g3)
    c: Horizontal(g2,g7)
    c: Horizontal(g1,g7)
    c: Horizontal(g5,g1)
    c: Tangent(g11,g10) = 1.5708
    c: Angle(g0) = -0.785398
    c: Radius(g8) = 10
    c: Coincident(g8,g-3)
    c: PointOnObject(g8,g0)
    c: Coincident(g9,g0)
    c: DistanceX(g5,g3) = 5
    c: DistanceX(g2,g7) = 5
    c: DistanceX(g11,g-1) = 5
    c: Coincident(g13,g12)
    c: Coincident(g13,g11)
    c: Vertical(g13)
    c: Coincident(g-4,g9)
    c: Coincident(g10,g-5)
    c: Distance(g0,g-4) = 5
    c: Coincident(g11,g-6)
    c: Vertical(g-4,g1)
    c: Vertical(g-5,g1)
    c: Coincident(g14,g15)
    c: Coincident(g15,g16)
    c: Coincident(g16,g17)
    c: Coincident(g17,g14)
    c: Horizontal(g14)
    c: Horizontal(g16)
    c: Vertical(g15)
    c: Vertical(g17)
    c: DistanceX(g-1,g16) = 8
    c: DistanceY(g-1,g16) = 5
    c: DistanceX(g14,g14) = 40.5
    c: DistanceY(g15,g15) = 20
FEATURE [PartDesign::Pocket] Pocket087  label="Leg and Servo Pockets"
  BaseFeature = -> Pad021
  Length = 20
  Length2 = 100
  Profile = -> Sketch117
  Type = 0
FEATURE [PartDesign::Fillet] Fillet031  label="Smooth Leg Pockets"
  Base = -> Pocket087 [Edge76,Edge72,Edge73,Edge75,Edge69,Edge70,Edge71,Edge68,Edge77,Edge81,Edge79,Edge80]
  BaseFeature = -> Pocket087
  Radius = 2
FEATURE [Sketcher::SketchObject] Sketch118
  MapMode = 5
  Placement = pos=(0,0,20) rot=(0,0,1;0rad)
  Support = -> [Fillet031]
  sketch-geometry (4):
    g0: LineSegment StartX=0 StartY=0 StartZ=0 EndX=56.5 EndY=0 EndZ=0
    g1: LineSegment StartX=56.5 StartY=0 StartZ=0 EndX=56.5 EndY=25 EndZ=0
    g2: LineSegment StartX=56.5 StartY=25 StartZ=0 EndX=0 EndY=25 EndZ=0
    g3: LineSegment StartX=0 StartY=25 StartZ=0 EndX=0 EndY=0 EndZ=0
  constraints (11):
    c: Coincident(g0,g1)
    c: Coincident(g1,g2)
    c: Coincident(g2,g3)
    c: Coincident(g3,g0)
    c: Horizontal(g0)
    c: Horizontal(g2)
    c: Vertical(g1)
    c: Vertical(g3)
    c: Coincident(g0,g-1)
    c: DistanceY(g3,g3) = 25
    c: DistanceX(g2,g2) = 56.5
FEATURE [PartDesign::Pocket] Pocket088  label="Counterpart Pocket"
  BaseFeature = -> Fillet031
  Length = 10
  Length2 = 100
  Profile = -> Sketch118
  Type = 0
FEATURE [PartDesign::Pad] Pad022  label="Extend Baseplate"
  BaseFeature = -> Pocket088
  Length = 12
  Length2 = 100
  Profile = -> Pocket088 [Face40]
  Type = 0
FEATURE [Sketcher::SketchObject] Sketch002
  MapMode = 5
  Placement = pos=(0,0,0) rot=(1,0,0;1.5708rad)
  Support = -> [XZ_Plane089]
  sketch-geometry (2):
    g0: Circle [constr] CenterX=0 CenterY=0 CenterZ=0 NormalX=0 NormalY=0 NormalZ=1 AngleXU=0 Radius=20
    g1: Circle CenterX=-20 CenterY=0 CenterZ=0 NormalX=0 NormalY=0 NormalZ=1 AngleXU=0 Radius=1.25
  constraints (5):
    c: Coincident(g0,g-1)
    c: Radius(g0) = 20
    c: PointOnObject(g1,g0)
    c: Radius(g1) = 1.25
    c: PointOnObject(g1,g-1)
FEATURE [Sketcher::SketchObject] Sketch119
  MapMode = 5
  Placement = pos=(0,0,32) rot=(0,0,1;0rad)
  Support = -> [Pad022]
  sketch-geometry (4):
    g0: LineSegment StartX=48.5 StartY=25 StartZ=0 EndX=56.5 EndY=25 EndZ=0
    g1: LineSegment StartX=56.5 StartY=25 StartZ=0 EndX=56.5 EndY=30 EndZ=0
    g2: LineSegment StartX=56.5 StartY=30 StartZ=0 EndX=48.5 EndY=30 EndZ=0
    g3: LineSegment StartX=48.5 StartY=30 StartZ=0 EndX=48.5 EndY=25 EndZ=0
  constraints (12):
    c: Coincident(g0,g1)
    c: Coincident(g1,g2)
    c: Coincident(g2,g3)
    c: Coincident(g3,g0)
    c: Horizontal(g0)
    c: Horizontal(g2)
    c: Vertical(g1)
    c: Vertical(g3)
    c: DistanceY(g3,g3) = 5
    c: DistanceY(g-1,g0) = 25
    c: DistanceX(g2,g2) = 8
    c: DistanceX(g-1,g2) = 48.5
FEATURE [PartDesign::Pocket] Pocket089  label="Remove Extension Servocover"
  BaseFeature = -> Pad022
  Length = 13
  Length2 = 100
  Profile = -> Sketch119
  Type = 0
FEATURE [Sketcher::SketchObject] Sketch120
  MapMode = 5
  Placement = pos=(0,30,0) rot=(0,0.707107,0.707107;3.14159rad)
  Support = -> [Pocket089]
  sketch-geometry (7):
    g0: ArcOfCircle CenterX=22.5 CenterY=65.1875 CenterZ=0 NormalX=0 NormalY=0 NormalZ=1 AngleXU=0 Radius=45.1875 StartAngle=4.19118 EndAngle=4.71239
    g1: LineSegment StartX=-56.5 StartY=33 StartZ=0 EndX=95 EndY=33 EndZ=0
    g2: LineSegment StartX=95 StartY=33 StartZ=0 EndX=95 EndY=20 EndZ=0
    g3: LineSegment StartX=95 StartY=20 StartZ=0 EndX=22.5 EndY=20 EndZ=0
    g4: ArcOfCircle CenterX=-22.5 CenterY=-13.1875 CenterZ=0 NormalX=0 NormalY=0 NormalZ=1 AngleXU=0 Radius=45.1875 StartAngle=1.04959 EndAngle=1.5708
    g5: LineSegment StartX=-22.5 StartY=32 StartZ=0 EndX=-56.5 EndY=32 EndZ=0
    g6: LineSegment StartX=-56.5 StartY=32 StartZ=0 EndX=-56.5 EndY=33 EndZ=0
  constraints (21):
    c: Horizontal(g1)
    c: Coincident(g2,g1)
    c: Vertical(g2)
    c: Coincident(g3,g2)
    c: Horizontal(g3)
    c: Tangent(g3,g0) = 1.5708
    c: DistanceX(g0,g0) = 22.5
    c: DistanceY(g0,g1) = 7
    c: DistanceY(g2,g2) = 13
    c: PointOnObject(g0,g-2)
    c: DistanceY(g-1,g2) = 20
    c: Tangent(g4,g0) = 1.5708
    c: Horizontal(g5)
    c: Coincident(g6,g5)
    c: Coincident(g1,g6)
    c: Vertical(g6)
    c: Tangent(g5,g4) = -1.5708
    c: DistanceY(g6,g6) = 1
    c: DistanceX(g5,g0) = 56.5
    c: DistanceX(g0,g1) = 95
    c: DistanceX(g4,g0) = 22.5
FEATURE [PartDesign::Pocket] Pocket090  label="Swing Leg"
  BaseFeature = -> Pocket089
  Length = 35
  Length2 = 100
  Profile = -> Sketch120
  Type = 0
FEATURE [PartDesign::Fillet] Fillet032  label="Servocable "
  Base = -> Pocket090 [Edge144,Edge135]
  BaseFeature = -> Pocket090
  Radius = 3
FEATURE [Sketcher::SketchObject] Sketch121
  ExternalGeometry = -> [Fillet032]
  MapMode = 5
  Placement = pos=(0,4.4e-15,20) rot=(0,0,1;0rad)
  Support = -> [Fillet032]
  sketch-geometry (12):
    g0: Circle CenterX=-82.3678 CenterY=12.6322 CenterZ=0 NormalX=0 NormalY=0 NormalZ=1 AngleXU=0 Radius=1.6
    g1: LineSegment [constr] StartX=-80 StartY=15 StartZ=0 EndX=-83.2345 EndY=15.8667 EndZ=0
    g2: LineSegment [constr] StartX=-83.2345 StartY=15.8667 StartZ=0 EndX=-85.6024 EndY=13.4988 EndZ=0
    g3: LineSegment [constr] StartX=-85.6024 StartY=13.4988 StartZ=0 EndX=-84.7357 EndY=10.2643 EndZ=0
    g4: LineSegment [constr] StartX=-84.7357 StartY=10.2643 StartZ=0 EndX=-81.5012 EndY=9.39763 EndZ=0
    g5: LineSegment [constr] StartX=-81.5012 StartY=9.39763 StartZ=0 EndX=-79.1333 EndY=11.7655 EndZ=0
    g6: LineSegment [constr] StartX=-79.1333 StartY=11.7655 StartZ=0 EndX=-80 EndY=15 EndZ=0
    g7: Circle [constr] CenterX=-82.3678 CenterY=12.6322 CenterZ=0 NormalX=0 NormalY=0 NormalZ=1 AngleXU=0 Radius=3.34863
    g8: Circle CenterX=4 CenterY=20 CenterZ=0 NormalX=0 NormalY=0 NormalZ=1 AngleXU=0 Radius=1.6
    g9: Circle CenterX=52.5 CenterY=20 CenterZ=0 NormalX=0 NormalY=0 NormalZ=1 AngleXU=0 Radius=1.6
    g10: Circle CenterX=52.5 CenterY=10 CenterZ=0 NormalX=0 NormalY=0 NormalZ=1 AngleXU=0 Radius=1.6
    g11: Circle CenterX=4 CenterY=10 CenterZ=0 NormalX=0 NormalY=0 NormalZ=1 AngleXU=0 Radius=1.6
  constraints (30):
    c: Radius(g0) = 1.6
    c: Coincident(g1,g2)
    c: Coincident(g2,g3)
    c: Coincident(g3,g4)
    c: Coincident(g4,g5)
    c: Coincident(g5,g6)
    c: Coincident(g6,g1)
    c: Equal(g1, g2-g6) x5
    c: PointOnObject(g1,g7)
    c: PointOnObject(g2,g7)
    c: PointOnObject(g3,g7)
    c: PointOnObject(g4,g7)
    c: PointOnObject(g5,g7)
    c: PointOnObject(g6,g7)
    c: Coincident(g7,g0)
    c: Distance(g4,g2) = 5.8
    c: Coincident(g1,g-3)
    c: Angle(g5) = 0.785398
    c: Horizontal(g8,g9)
    c: Horizontal(g11,g10)
    c: Vertical(g10,g9)
    c: Vertical(g8,g11)
    c: Equal(g11,g8)
    c: Equal(g8,g9)
    c: Equal(g9,g10)
    c: Equal(g8,g0)
    c: DistanceX(g11,g10) = 48.5
    c: DistanceY(g11,g8) = 10
    c: DistanceY(g-1,g11) = 10
    c: DistanceX(g-1,g11) = 4
FEATURE [PartDesign::Pocket] Pocket091  label="Screwhole"
  BaseFeature = -> Fillet032
  Length = 20
  Length2 = 100
  Profile = -> Sketch121
  Type = 0
FEATURE [Sketcher::SketchObject] Sketch122
  MapMode = 5
  Placement = pos=(0,4.4e-15,20) rot=(0,0,1;0rad)
  Support = -> [Pocket091]
  sketch-geometry (5):
    g0: ArcOfCircle CenterX=-80 CenterY=15 CenterZ=0 NormalX=0 NormalY=0 NormalZ=1 AngleXU=0 Radius=12.5 StartAngle=2.35619 EndAngle=5.49779
    g1: LineSegment [constr] StartX=-88.8388 StartY=23.8388 StartZ=0 EndX=-71.1612 EndY=6.16117 EndZ=0
    g2: LineSegment StartX=-88.8388 StartY=23.8388 StartZ=0 EndX=-92.3744 EndY=27.3744 EndZ=0
    g3: LineSegment StartX=-71.1612 StartY=6.16117 StartZ=0 EndX=-67.6256 EndY=2.62563 EndZ=0
    g4: ArcOfCircle CenterX=-80 CenterY=15 CenterZ=0 NormalX=0 NormalY=0 NormalZ=1 AngleXU=0 Radius=17.5 StartAngle=2.35619 EndAngle=5.49779
  constraints (15):
    c: Radius(g0) = 12.5
    c: DistanceX(g0,g-1) = 80
    c: DistanceY(g-1,g0) = 15
    c: Coincident(g1,g0)
    c: Coincident(g1,g0)
    c: Angle(g1) = -0.785398
    c: PointOnObject(g0,g1)
    c: Coincident(g2,g0)
    c: Coincident(g3,g0)
    c: Coincident(g4,g0)
    c: Coincident(g4,g2)
    c: Coincident(g4,g3)
    c: Tangent(g2,g1)
    c: Tangent(g1,g3)
    c: Radius(g4) = 17.5
FEATURE [PartDesign::Pocket] Pocket092  label="Rubberfoot Pocket"
  BaseFeature = -> Pocket091
  Length = 20
  Length2 = 100
  Profile = -> Sketch122
  Type = 0
FEATURE [Sketcher::SketchObject] Sketch123
  AttachmentOffset = pos=(0,0,-17) rot=(0,0,1;0rad)
  ExternalGeometry = -> [Pocket092]
  MapMode = 5
  Placement = pos=(0,7e-16,3) rot=(0,0,1;0rad)
  Support = -> [Pocket092]
  sketch-geometry (10):
    g0: LineSegment [constr] StartX=-80 StartY=15 StartZ=0 EndX=-83.2345 EndY=15.8667 EndZ=0
    g1: LineSegment StartX=-83.2345 StartY=15.8667 StartZ=0 EndX=-85.6024 EndY=13.4988 EndZ=0
    g2: LineSegment StartX=-85.6024 StartY=13.4988 StartZ=0 EndX=-84.7357 EndY=10.2643 EndZ=0
    g3: LineSegment StartX=-84.7357 StartY=10.2643 StartZ=0 EndX=-81.5012 EndY=9.39763 EndZ=0
    g4: LineSegment StartX=-81.5012 StartY=9.39763 StartZ=0 EndX=-79.1333 EndY=11.7655 EndZ=0
    g5: LineSegment [constr] StartX=-79.1333 StartY=11.7655 StartZ=0 EndX=-80 EndY=15 EndZ=0
    g6: Circle [constr] CenterX=-82.3678 CenterY=12.6322 CenterZ=0 NormalX=0 NormalY=0 NormalZ=1 AngleXU=0 Radius=3.34863
    g7: LineSegment StartX=-79.1333 StartY=11.7655 StartZ=0 EndX=-77.7191 EndY=13.1797 EndZ=0
    g8: LineSegment StartX=-77.7191 StartY=13.1797 StartZ=0 EndX=-81.8203 EndY=17.2809 EndZ=0
    g9: LineSegment StartX=-81.8203 StartY=17.2809 StartZ=0 EndX=-83.2345 EndY=15.8667 EndZ=0
  constraints (23):
    c: Coincident(g0,g1)
    c: Coincident(g1,g2)
    c: Coincident(g2,g3)
    c: Coincident(g3,g4)
    c: Coincident(g4,g5)
    c: Coincident(g5,g0)
    c: Equal(g0, g1-g5) x5
    c: PointOnObject(g0,g6)
    c: PointOnObject(g1,g6)
    c: PointOnObject(g2,g6)
    c: PointOnObject(g3,g6)
    c: PointOnObject(g4,g6)
    c: PointOnObject(g5,g6)
    c: Coincident(g6,g-3)
    c: Angle(g4) = 0.785398
    c: Distance(g1,g3) = 5.8
    c: Coincident(g8,g7)
    c: Coincident(g9,g8)
    c: Coincident(g9,g0)
    c: Tangent(g7,g4) = -1.5708
    c: Tangent(g9,g1)
    c: Perpendicular(g8,g7)
    c: Distance(g7) = 2
FEATURE [Sketcher::SketchObject] Sketch315
  AttachmentOffset = pos=(0,0,-3) rot=(0,0,1;0rad)
  ExternalGeometry = -> [Pocket092]
  MapMode = 5
  Placement = pos=(0,3.7e-15,17) rot=(0,0,1;0rad)
  Support = -> [Pocket092]
  sketch-geometry (10):
    g0: LineSegment [constr] StartX=-80 StartY=15 StartZ=0 EndX=-83.2345 EndY=15.8667 EndZ=0
    g1: LineSegment StartX=-83.2345 StartY=15.8667 StartZ=0 EndX=-85.6024 EndY=13.4988 EndZ=0
    g2: LineSegment StartX=-85.6024 StartY=13.4988 StartZ=0 EndX=-84.7357 EndY=10.2643 EndZ=0
    g3: LineSegment StartX=-84.7357 StartY=10.2643 StartZ=0 EndX=-81.5012 EndY=9.39763 EndZ=0
    g4: LineSegment StartX=-81.5012 StartY=9.39763 StartZ=0 EndX=-79.1333 EndY=11.7655 EndZ=0
    g5: LineSegment [constr] StartX=-79.1333 StartY=11.7655 StartZ=0 EndX=-80 EndY=15 EndZ=0
    g6: Circle [constr] CenterX=-82.3678 CenterY=12.6322 CenterZ=0 NormalX=0 NormalY=0 NormalZ=1 AngleXU=0 Radius=3.34863
    g7: LineSegment StartX=-79.1333 StartY=11.7655 StartZ=0 EndX=-77.7191 EndY=13.1797 EndZ=0
    g8: LineSegment StartX=-77.7191 StartY=13.1797 StartZ=0 EndX=-81.8203 EndY=17.2809 EndZ=0
    g9: LineSegment StartX=-81.8203 StartY=17.2809 StartZ=0 EndX=-83.2345 EndY=15.8667 EndZ=0
  constraints (23):
    c: Coincident(g0,g1)
    c: Coincident(g1,g2)
    c: Coincident(g2,g3)
    c: Coincident(g3,g4)
    c: Coincident(g4,g5)
    c: Coincident(g5,g0)
    c: Equal(g0, g1-g5) x5
    c: PointOnObject(g0,g6)
    c: PointOnObject(g1,g6)
    c: PointOnObject(g2,g6)
    c: PointOnObject(g3,g6)
    c: PointOnObject(g4,g6)
    c: PointOnObject(g5,g6)
    c: Coincident(g6,g-3)
    c: Angle(g4) = 0.785398
    c: Distance(g1,g3) = 5.8
    c: Coincident(g8,g7)
    c: Coincident(g9,g8)
    c: Coincident(g9,g0)
    c: Tangent(g7,g4) = -1.5708
    c: Tangent(g9,g1)
    c: Perpendicular(g8,g7)
    c: Distance(g7) = 2
FEATURE [PartDesign::Pocket] Pocket139  label="Nuthole #1"
  BaseFeature = -> Pocket092
  Length = 3
  Length2 = 100
  Profile = -> Sketch315
  Type = 0
FEATURE [PartDesign::Pocket] Pocket093  label="Nuthole #2"
  BaseFeature = -> Pocket139
  Length = 3
  Length2 = 100
  Profile = -> Sketch123
  Reversed = true
  Type = 0
FEATURE [PartDesign::Chamfer] Chamfer  label="Smooth Nutholes"
  Base = -> Pocket093 [Edge206,Edge207,Edge141,Edge209,Edge208,Edge225,Edge222,Edge223,Edge224,Edge221]
  BaseFeature = -> Pocket093
  Size = 0.625
FEATURE [Sketcher::SketchObject] Sketch124
  MapMode = 5
  Placement = pos=(0,0,10) rot=(0,0,1;0rad)
  Support = -> [Chamfer]
  sketch-geometry (4):
    g0: LineSegment StartX=0 StartY=0 StartZ=0 EndX=56.5 EndY=0 EndZ=0
    g1: LineSegment StartX=56.5 StartY=0 StartZ=0 EndX=56.5 EndY=5 EndZ=0
    g2: LineSegment StartX=56.5 StartY=5 StartZ=0 EndX=0 EndY=5 EndZ=0
    g3: LineSegment StartX=0 StartY=5 StartZ=0 EndX=0 EndY=0 EndZ=0
  constraints (11):
    c: Coincident(g0,g1)
    c: Coincident(g1,g2)
    c: Coincident(g2,g3)
    c: Coincident(g3,g0)
    c: Horizontal(g0)
    c: Horizontal(g2)
    c: Vertical(g1)
    c: Vertical(g3)
    c: Coincident(g0,g-1)
    c: DistanceY(g1,g1) = 5
    c: DistanceX(g2,g2) = 56.5
FEATURE [PartDesign::Pocket] Pocket094  label="Shorten Baseplate"
  BaseFeature = -> Chamfer
  Length = 10
  Length2 = 100
  Profile = -> Sketch124
  Type = 0
FEATURE [PartDesign::Fillet] Fillet050  label="Smooth Corners"
  Base = -> Pocket094 [Edge232,Edge234,Edge240,Edge242,Edge193,Edge83,Edge85,Edge86,Edge88,Edge170,Edge236,Edge238,Edge258]
  BaseFeature = -> Pocket094
  Radius = 0.4
FEATURE [Sketcher::SketchObject] Sketch125
  MapMode = 5
  Placement = pos=(0,0,0) rot=(1,0,0;1.5708rad)
  Support = -> [XZ_Plane089]
  sketch-geometry (2):
    g0: ArcOfCircle CenterX=0 CenterY=0 CenterZ=0 NormalX=0 NormalY=0 NormalZ=1 AngleXU=0 Radius=20 StartAngle=-1.8e-15 EndAngle=3.14159
    g1: LineSegment StartX=-20 StartY=-1.38798e-11 StartZ=0 EndX=20 EndY=-3.55e-14 EndZ=0
  constraints (6):
    c: Coincident(g0,g-1)
    c: PointOnObject(g0,g-1)
    c: PointOnObject(g0,g-1)
    c: Coincident(g1,g0)
    c: Coincident(g1,g0)
    c: Radius(g0) = 20
FEATURE [PartDesign::Pad] Pad098  label="Baseblock"
  Length = 15
  Length2 = 15
  Placement = pos=(0,0,0) rot=(1,0,0;1.5708rad)
  Profile = -> Sketch125
  Type = 4
FEATURE [Sketcher::SketchObject] Sketch005
  MapMode = 5
  Placement = pos=(0,0,0) rot=(1,0,0;1.5708rad)
  Support = -> [XZ_Plane089]
  sketch-geometry (2):
    g0: ArcOfCircle CenterX=0 CenterY=0 CenterZ=0 NormalX=0 NormalY=0 NormalZ=1 AngleXU=0 Radius=12.75 StartAngle=0 EndAngle=3.14159
    g1: LineSegment StartX=-12.75 StartY=0 StartZ=0 EndX=12.75 EndY=0 EndZ=0
  constraints (6):
    c: Coincident(g0,g-1)
    c: Coincident(g1,g0)
    c: Coincident(g1,g0)
    c: Horizontal(g1)
    c: PointOnObject(g0,g1)
    c: Radius(g0) = 12.75
FEATURE [Sketcher::SketchObject] Sketch007
  MapMode = 5
  Placement = pos=(0,0,0) rot=(1,0,0;1.5708rad)
  Support = -> [XZ_Plane089]
  sketch-geometry (8):
    g0: LineSegment [constr] StartX=-4e-16 StartY=6.69726 StartZ=0 EndX=-2.9 EndY=5.02295 EndZ=0
    g1: LineSegment [constr] StartX=-2.9 StartY=5.02295 StartZ=0 EndX=-2.9 EndY=1.67432 EndZ=0
    g2: LineSegment [constr] StartX=-2.9 StartY=1.67432 StartZ=0 EndX=0 EndY=0 EndZ=0
    g3: LineSegment [constr] StartX=0 StartY=0 StartZ=0 EndX=2.9 EndY=1.67432 EndZ=0
    g4: LineSegment [constr] StartX=2.9 StartY=1.67432 StartZ=0 EndX=2.9 EndY=5.02295 EndZ=0
    g5: LineSegment [constr] StartX=2.9 StartY=5.02295 StartZ=0 EndX=-4e-16 EndY=6.69726 EndZ=0
    g6: Circle [constr] CenterX=0 CenterY=3.34863 CenterZ=0 NormalX=0 NormalY=0 NormalZ=1 AngleXU=0 Radius=3.34863
    g7: Circle CenterX=0 CenterY=3.34863 CenterZ=0 NormalX=0 NormalY=0 NormalZ=1 AngleXU=0 Radius=1.6
  constraints (18):
    c: Coincident(g0,g1)
    c: Coincident(g1,g2)
    c: Coincident(g2,g3)
    c: Coincident(g3,g4)
    c: Coincident(g4,g5)
    c: Coincident(g5,g0)
    c: Equal(g0, g1-g5) x5
    c: PointOnObject(g0,g6)
    c: PointOnObject(g1,g6)
    c: PointOnObject(g2,g6)
    c: PointOnObject(g3,g6)
    c: PointOnObject(g4,g6)
    c: PointOnObject(g5,g6)
    c: PointOnObject(g6,g-2)
    c: DistanceX(g0,g4) = 5.8
    c: Coincident(g2,g-1)
    c: Coincident(g7,g6)
    c: Radius(g7) = 1.6
FEATURE [Sketcher::SketchObject] Sketch003
  MapMode = 5
  Support = -> [XY_Plane088]
  sketch-geometry (3):
    g0: Circle [constr] CenterX=0 CenterY=0 CenterZ=0 NormalX=0 NormalY=0 NormalZ=1 AngleXU=0 Radius=20
    g1: Circle CenterX=18.1039 CenterY=8.5 CenterZ=0 NormalX=0 NormalY=0 NormalZ=1 AngleXU=0 Radius=1.25
    g2: Circle CenterX=18.1039 CenterY=-8.5 CenterZ=0 NormalX=0 NormalY=0 NormalZ=1 AngleXU=0 Radius=1.25
  constraints (7):
    c: Coincident(g0,g-1)
    c: Radius(g0) = 20
    c: PointOnObject(g1,g0)
    c: Radius(g1) = 1.25
    c: DistanceY(g-1,g1) = 8.5
    c: Equal(g2,g1)
    c: Symmetric(g2,g1,g-1)
FEATURE [Sketcher::SketchObject] Sketch006
  MapMode = 5
  Placement = pos=(0,0,0) rot=(1,0,0;1.5708rad)
  Support = -> [XZ_Plane089]
  sketch-geometry (6):
    g0: LineSegment StartX=-15 StartY=0 StartZ=0 EndX=-25 EndY=7.5 EndZ=0
    g1: LineSegment StartX=-25 StartY=7.5 StartZ=0 EndX=-25 EndY=-7.5 EndZ=0
    g2: LineSegment StartX=-25 StartY=-7.5 StartZ=0 EndX=25 EndY=-7.5 EndZ=0
    g3: LineSegment StartX=25 StartY=-7.5 StartZ=0 EndX=25 EndY=7.5 EndZ=0
    g4: LineSegment StartX=25 StartY=7.5 StartZ=0 EndX=15 EndY=0 EndZ=0
    g5: LineSegment StartX=15 StartY=0 StartZ=0 EndX=-15 EndY=0 EndZ=0
  constraints (15):
    c: PointOnObject(g0,g-1)
    c: Coincident(g0,g1)
    c: Vertical(g1)
    c: Coincident(g1,g2)
    c: Horizontal(g2)
    c: Coincident(g2,g3)
    c: Coincident(g3,g4)
    c: Coincident(g4,g5)
    c: Coincident(g5,g0)
    c: DistanceX(g5,g5) = 30
    c: DistanceX(g4,g2) = 10
    c: Symmetric(g0,g4,g-2)
    c: Symmetric(g0,g3,g-2)
    c: DistanceY(g-1,g3) = 7.5
    c: Symmetric(g2,g3,g-1)
FEATURE [Sketcher::SketchObject] Sketch004
  MapMode = 5
  Support = -> [XY_Plane088]
  sketch-geometry (8):
    g0: LineSegment StartX=-20 StartY=14 StartZ=0 EndX=20 EndY=14 EndZ=0
    g1: LineSegment StartX=20 StartY=14 StartZ=0 EndX=20 EndY=19 EndZ=0
    g2: LineSegment StartX=20 StartY=19 StartZ=0 EndX=-20 EndY=19 EndZ=0
    g3: LineSegment StartX=-20 StartY=19 StartZ=0 EndX=-20 EndY=14 EndZ=0
    g4: LineSegment StartX=-20 StartY=-19 StartZ=0 EndX=20 EndY=-19 EndZ=0
    g5: LineSegment StartX=20 StartY=-19 StartZ=0 EndX=20 EndY=-14 EndZ=0
    g6: LineSegment StartX=20 StartY=-14 StartZ=0 EndX=-20 EndY=-14 EndZ=0
    g7: LineSegment StartX=-20 StartY=-14 StartZ=0 EndX=-20 EndY=-19 EndZ=0
  constraints (22):
    c: Coincident(g0,g1)
    c: Coincident(g1,g2)
    c: Coincident(g2,g3)
    c: Coincident(g3,g0)
    c: Horizontal(g0)
    c: Vertical(g1)
    c: Vertical(g3)
    c: Coincident(g4,g5)
    c: Coincident(g5,g6)
    c: Coincident(g6,g7)
    c: Coincident(g7,g4)
    c: Horizontal(g4)
    c: Horizontal(g6)
    c: Vertical(g5)
    c: Vertical(g7)
    c: Equal(g1,g5)
    c: Equal(g6,g2)
    c: Symmetric(g1,g2,g-2)
    c: Symmetric(g1,g4,g-1)
    c: DistanceY(g1,g1) = 5
    c: DistanceY(g5,g0) = 28
    c: DistanceX(g2,g2) = 40
FEATURE [Sketcher::SketchObject] Sketch126
  MapMode = 5
  Support = -> [XY_Plane003]
  sketch-geometry (8):
    g0: LineSegment StartX=0 StartY=3.17543 StartZ=0 EndX=-2.75 EndY=1.58771 EndZ=0
    g1: LineSegment StartX=-2.75 StartY=1.58771 StartZ=0 EndX=-2.75 EndY=-1.58771 EndZ=0
    g2: LineSegment StartX=-2.75 StartY=-1.58771 StartZ=0 EndX=0 EndY=-3.17543 EndZ=0
    g3: LineSegment StartX=0 StartY=-3.17543 StartZ=0 EndX=2.75 EndY=-1.58771 EndZ=0
    g4: LineSegment StartX=2.75 StartY=-1.58771 StartZ=0 EndX=2.75 EndY=1.58771 EndZ=0
    g5: LineSegment StartX=2.75 StartY=1.58771 StartZ=0 EndX=0 EndY=3.17543 EndZ=0
    g6: Circle [constr] CenterX=0 CenterY=0 CenterZ=0 NormalX=0 NormalY=0 NormalZ=1 AngleXU=0 Radius=3.17543
    g7: Circle CenterX=0 CenterY=0 CenterZ=0 NormalX=0 NormalY=0 NormalZ=1 AngleXU=0 Radius=1.5
  constraints (18):
    c: Coincident(g0,g1)
    c: Coincident(g1,g2)
    c: Coincident(g2,g3)
    c: Coincident(g3,g4)
    c: Coincident(g4,g5)
    c: Coincident(g5,g0)
    c: Equal(g0, g1-g5) x5
    c: PointOnObject(g0,g6)
    c: PointOnObject(g1,g6)
    c: PointOnObject(g2,g6)
    c: PointOnObject(g3,g6)
    c: PointOnObject(g4,g6)
    c: PointOnObject(g5,g6)
    c: Coincident(g6,g-1)
    c: PointOnObject(g5,g-2)
    c: DistanceX(g0,g4) = 5.5
    c: Coincident(g7,g-1)
    c: Radius(g7) = 1.5
FEATURE [PartDesign::Pad] Pad023  label="M3 Nut Primitive"
  Length = 1.2
  Length2 = 1.2
  Profile = -> Sketch126
  Type = 4
FEATURE [Sketcher::SketchObject] Sketch127
  ExternalGeometry = -> [Pad023]
  MapMode = 5
  Placement = pos=(0,0,0) rot=(0.57735,0.57735,0.57735;2.0944rad)
  Support = -> [YZ_Plane003]
  sketch-geometry (6):
    g0: LineSegment StartX=-2.67543 StartY=1.2 StartZ=0 EndX=-3.67543 EndY=1.2 EndZ=0
    g1: LineSegment StartX=-3.67543 StartY=1.2 StartZ=0 EndX=-3.67543 EndY=-1.2 EndZ=0
    g2: LineSegment StartX=-3.67543 StartY=-1.2 StartZ=0 EndX=-2.67543 EndY=-1.2 EndZ=0
    g3: LineSegment StartX=-2.67543 StartY=-1.2 StartZ=0 EndX=-3.17543 EndY=-1 EndZ=0
    g4: LineSegment StartX=-3.17543 StartY=-1 StartZ=0 EndX=-3.17543 EndY=1 EndZ=0
    g5: LineSegment StartX=-3.17543 StartY=1 StartZ=0 EndX=-2.67543 EndY=1.2 EndZ=0
  constraints (15):
    c: Horizontal(g0)
    c: Coincident(g0,g1)
    c: Coincident(g1,g2)
    c: Coincident(g2,g3)
    c: Coincident(g3,g4)
    c: Coincident(g4,g5)
    c: Coincident(g5,g0)
    c: Symmetric(g4,g3,g-1)
    c: Symmetric(g0,g2,g-1)
    c: Symmetric(g1,g0,g-1)
    c: DistanceX(g0,g4) = 0.5
    c: DistanceY(g3,g4) = 2
    c: DistanceY(g1,g0) = 2.4
    c: PointOnObject(g3,g-3)
    c: DistanceX(g4,g0) = 0.5
FEATURE [PartDesign::Groove] Groove019  label="M3 Nut Smooth"
  Angle = 360
  Axis = (-2e-16,3e-16,1)
  Base = (0,0,0)
  BaseFeature = -> Pad023
  Profile = -> Sketch127
  ReferenceAxis = -> Sketch127 [V_Axis]
  Reversed = true
FEATURE [PartDesign::Chamfer] Chamfer001  label="M3 Nut Smooth Hole"
  Base = -> Groove019 [Edge24,Edge23]
  BaseFeature = -> Groove019
  Size = 0.2
FEATURE [Sketcher::SketchObject] Sketch318
  MapMode = 5
  Placement = pos=(0,0,-6.9576e-12) rot=(1,0,0;3.14159rad)
  Support = -> [Pad098]
  sketch-geometry (4):
    g0: ArcOfCircle CenterX=0 CenterY=0 CenterZ=0 NormalX=0 NormalY=0 NormalZ=1 AngleXU=0 Radius=20 StartAngle=2.29353 EndAngle=3.98965
    g1: LineSegment StartX=-13.2288 StartY=15 StartZ=0 EndX=-23.2288 EndY=15 EndZ=0
    g2: LineSegment StartX=-23.2288 StartY=15 StartZ=0 EndX=-23.2288 EndY=-15 EndZ=0
    g3: LineSegment StartX=-23.2288 StartY=-15 StartZ=0 EndX=-13.2288 EndY=-15 EndZ=0
  constraints (12):
    c: Coincident(g0,g-1)
    c: Vertical(g0,g0)
    c: Coincident(g0,g1)
    c: Coincident(g1,g2)
    c: Vertical(g2)
    c: Coincident(g2,g3)
    c: Coincident(g3,g0)
    c: Horizontal(g3)
    c: Radius(g0) = 20
    c: DistanceX(g1,g1) = 10
    c: DistanceY(g2,g2) = 30
    c: Horizontal(g1)
FEATURE [PartDesign::Groove] Groove  label="Halfspherical Shape"
  Angle = 360
  Axis = (0,-1,7e-16)
  Base = (0,0,-6.9577e-12)
  BaseFeature = -> Pad098
  Placement = pos=(0,0,0) rot=(1,0,0;1.5708rad)
  Profile = -> Sketch318
  ReferenceAxis = -> Sketch318 [V_Axis]
  Reversed = true
FEATURE [PartDesign::SubtractivePipe] SubtractivePipe003  label="Horizontal Profile"
  AuxilleryCurvelinear = true
  AuxillerySpineTangent = false
  BaseFeature = -> Groove
  Binormal = (0,0,0)
  Mode = 0
  Placement = pos=(0,0,0) rot=(1,0,0;1.5708rad)
  Profile = -> Sketch002
  Spine = -> Groove [Edge2,Edge1]
  SpineTangent = false
  Transformation = 0
  Transition = 0
FEATURE [PartDesign::PolarPattern] PolarPattern  label="Horizontal Profile Polar Pattern"
  Angle = 180
  Axis = -> Sketch002 [N_Axis]
  BaseFeature = -> SubtractivePipe003
  Occurrences = 12
  Originals = -> [SubtractivePipe003]
  Placement = pos=(0,0,0) rot=(1,0,0;1.5708rad)
  Reversed = true
FEATURE [PartDesign::Groove] Groove015  label="Vertical Profiles"
  Angle = 360
  Axis = (0,1,0)
  Base = (0,0,0)
  BaseFeature = -> PolarPattern
  Placement = pos=(0,0,0) rot=(1,0,0;1.5708rad)
  Profile = -> Sketch003
  ReferenceAxis = -> Sketch003 [V_Axis]
FEATURE [PartDesign::Pocket] Pocket095  label="Cut Sides"
  BaseFeature = -> Groove015
  Length = 25
  Length2 = 100
  Placement = pos=(0,0,0) rot=(1,0,0;1.5708rad)
  Profile = -> Sketch004
  Reversed = true
  Type = 0
FEATURE [PartDesign::Pocket] Pocket141  label="Inner Halfspherical Cutout"
  BaseFeature = -> Pocket095
  Length = 10
  Length2 = 10
  Placement = pos=(0,0,0) rot=(1,0,0;1.5708rad)
  Profile = -> Sketch005
  Type = 4
FEATURE [PartDesign::Pocket] Pocket142  label="Slanted Edge"
  BaseFeature = -> Pocket141
  Length = 15
  Length2 = 15
  Placement = pos=(0,0,0) rot=(1,0,0;1.5708rad)
  Profile = -> Sketch006
  Type = 4
FEATURE [PartDesign::Pocket] Pocket140  label="Screwholes"
  BaseFeature = -> Pocket142
  Length = 15
  Length2 = 15
  Placement = pos=(0,0,0) rot=(1,0,0;1.5708rad)
  Profile = -> Sketch007
  Type = 4
FEATURE [Sketcher::SketchObject] Sketch316
  ExternalGeometry = -> [Pocket140]
  MapMode = 5
  Placement = pos=(0,14,-6.2e-15) rot=(-1,0,0;1.5708rad)
  Support = -> [Pocket140]
  sketch-geometry (1):
    g0: Circle CenterX=0 CenterY=-3.34863 CenterZ=0 NormalX=0 NormalY=0 NormalZ=1 AngleXU=0 Radius=2.85
  constraints (2):
    c: Coincident(g0,g-3)
    c: Radius(g0) = 2.85
FEATURE [PartDesign::Pocket] Pocket143  label="Screwhead Left"
  BaseFeature = -> Pocket140
  Length = 2.5
  Length2 = 100
  Placement = pos=(0,0,0) rot=(1,0,0;1.5708rad)
  Profile = -> Sketch316
  Type = 0
FEATURE [Sketcher::SketchObject] Sketch314
  ExternalGeometry = -> [Pocket143]
  MapMode = 5
  Placement = pos=(0,-14,6.2e-15) rot=(1,0,0;1.5708rad)
  Support = -> [Pocket143]
  sketch-geometry (1):
    g0: Circle CenterX=0 CenterY=3.34863 CenterZ=0 NormalX=0 NormalY=0 NormalZ=1 AngleXU=0 Radius=2.85
  constraints (2):
    c: Coincident(g-3,g0)
    c: Radius(g0) = 2.85
FEATURE [PartDesign::Pocket] Pocket005  label="Screwhead Right"
  BaseFeature = -> Pocket143
  Length = 2.5
  Length2 = 100
  Placement = pos=(0,0,0) rot=(1,0,0;1.5708rad)
  Profile = -> Sketch314
  Type = 0
FEATURE [Sketcher::SketchObject] Sketch128
  MapMode = 5
  Support = -> [XY_Plane089]
  sketch-geometry (8):
    g0: LineSegment StartX=0 StartY=3.17543 StartZ=0 EndX=-2.75 EndY=1.58771 EndZ=0
    g1: LineSegment StartX=-2.75 StartY=1.58771 StartZ=0 EndX=-2.75 EndY=-1.58771 EndZ=0
    g2: LineSegment StartX=-2.75 StartY=-1.58771 StartZ=0 EndX=0 EndY=-3.17543 EndZ=0
    g3: LineSegment StartX=0 StartY=-3.17543 StartZ=0 EndX=2.75 EndY=-1.58771 EndZ=0
    g4: LineSegment StartX=2.75 StartY=-1.58771 StartZ=0 EndX=2.75 EndY=1.58771 EndZ=0
    g5: LineSegment StartX=2.75 StartY=1.58771 StartZ=0 EndX=0 EndY=3.17543 EndZ=0
    g6: Circle [constr] CenterX=0 CenterY=0 CenterZ=0 NormalX=0 NormalY=0 NormalZ=1 AngleXU=0 Radius=3.17543
    g7: Circle CenterX=0 CenterY=0 CenterZ=0 NormalX=0 NormalY=0 NormalZ=1 AngleXU=0 Radius=1.5
  constraints (18):
    c: Coincident(g0,g1)
    c: Coincident(g1,g2)
    c: Coincident(g2,g3)
    c: Coincident(g3,g4)
    c: Coincident(g4,g5)
    c: Coincident(g5,g0)
    c: Equal(g0, g1-g5) x5
    c: PointOnObject(g0,g6)
    c: PointOnObject(g1,g6)
    c: PointOnObject(g2,g6)
    c: PointOnObject(g3,g6)
    c: PointOnObject(g4,g6)
    c: PointOnObject(g5,g6)
    c: Coincident(g6,g-1)
    c: PointOnObject(g5,g-2)
    c: DistanceX(g0,g4) = 5.5
    c: Coincident(g7,g-1)
    c: Radius(g7) = 1.5
FEATURE [PartDesign::Pad] Pad024  label="M3 Nut Primitive018"
  Length = 1.2
  Length2 = 1.2
  Profile = -> Sketch128
  Type = 4
FEATURE [Sketcher::SketchObject] Sketch129
  ExternalGeometry = -> [Pad024]
  MapMode = 5
  Placement = pos=(0,0,0) rot=(0.57735,0.57735,0.57735;2.0944rad)
  Support = -> [YZ_Plane088]
  sketch-geometry (6):
    g0: LineSegment StartX=-2.67543 StartY=1.2 StartZ=0 EndX=-3.67543 EndY=1.2 EndZ=0
    g1: LineSegment StartX=-3.67543 StartY=1.2 StartZ=0 EndX=-3.67543 EndY=-1.2 EndZ=0
    g2: LineSegment StartX=-3.67543 StartY=-1.2 StartZ=0 EndX=-2.67543 EndY=-1.2 EndZ=0
    g3: LineSegment StartX=-2.67543 StartY=-1.2 StartZ=0 EndX=-3.17543 EndY=-1 EndZ=0
    g4: LineSegment StartX=-3.17543 StartY=-1 StartZ=0 EndX=-3.17543 EndY=1 EndZ=0
    g5: LineSegment StartX=-3.17543 StartY=1 StartZ=0 EndX=-2.67543 EndY=1.2 EndZ=0
  constraints (15):
    c: Horizontal(g0)
    c: Coincident(g0,g1)
    c: Coincident(g1,g2)
    c: Coincident(g2,g3)
    c: Coincident(g3,g4)
    c: Coincident(g4,g5)
    c: Coincident(g5,g0)
    c: Symmetric(g4,g3,g-1)
    c: Symmetric(g0,g2,g-1)
    c: Symmetric(g1,g0,g-1)
    c: DistanceX(g0,g4) = 0.5
    c: DistanceY(g3,g4) = 2
    c: DistanceY(g1,g0) = 2.4
    c: PointOnObject(g3,g-3)
    c: DistanceX(g4,g0) = 0.5
FEATURE [PartDesign::Groove] Groove020  label="M3 Nut Smooth018"
  Angle = 360
  Axis = (-2e-16,3e-16,1)
  Base = (0,0,0)
  BaseFeature = -> Pad024
  Profile = -> Sketch129
  ReferenceAxis = -> Sketch129 [V_Axis]
  Reversed = true
FEATURE [PartDesign::Chamfer] Chamfer002  label="M3 Nut Smooth Hole018"
  Base = -> Groove020 [Edge24,Edge23]
  BaseFeature = -> Groove020
  Size = 0.2
FEATURE [Sketcher::SketchObject] Sketch130
  MapMode = 5
  Support = -> [XY_Plane011]
  sketch-geometry (1):
    g0: Circle CenterX=0 CenterY=0 CenterZ=0 NormalX=0 NormalY=0 NormalZ=1 AngleXU=0 Radius=2.75
  constraints (2):
    c: Coincident(g0,g-1)
    c: Radius(g0) = 2.75
FEATURE [PartDesign::Pad] Pad001  label="M3x8 Head"
  Length = 3
  Length2 = 100
  Profile = -> Sketch130
  Type = 0
FEATURE [Sketcher::SketchObject] Sketch132
  MapMode = 5
  Placement = pos=(0,0,3) rot=(0,0,1;0rad)
  Support = -> [Pad001]
  sketch-geometry (1):
    g0: Circle CenterX=0 CenterY=0 CenterZ=0 NormalX=0 NormalY=0 NormalZ=1 AngleXU=0 Radius=1.5
  constraints (2):
    c: Coincident(g0,g-1)
    c: Radius(g0) = 1.5
FEATURE [PartDesign::Pad] Pad002  label="M3x8 Thread"
  BaseFeature = -> Pad001
  Length = 8
  Length2 = 100
  Profile = -> Sketch132
  Type = 0
FEATURE [Sketcher::SketchObject] Sketch319
  MapMode = 5
  Support = -> [XY_Plane012]
  sketch-geometry (1):
    g0: Circle CenterX=0 CenterY=0 CenterZ=0 NormalX=0 NormalY=0 NormalZ=1 AngleXU=0 Radius=2.75
  constraints (2):
    c: Coincident(g0,g-1)
    c: Radius(g0) = 2.75
FEATURE [PartDesign::Pad] Pad026  label="M3x8 Head014"
  Length = 3
  Length2 = 100
  Profile = -> Sketch319
  Type = 0
FEATURE [Sketcher::SketchObject] Sketch317
  MapMode = 5
  Placement = pos=(0,0,3) rot=(0,0,1;0rad)
  Support = -> [Pad026]
  sketch-geometry (1):
    g0: Circle CenterX=0 CenterY=0 CenterZ=0 NormalX=0 NormalY=0 NormalZ=1 AngleXU=0 Radius=1.5
  constraints (2):
    c: Coincident(g0,g-1)
    c: Radius(g0) = 1.5
FEATURE [PartDesign::Pad] Pad025  label="M3x8 Thread014"
  BaseFeature = -> Pad026
  Length = 8
  Length2 = 100
  Profile = -> Sketch317
  Type = 0
FEATURE [Sketcher::SketchObject] Sketch131
  MapMode = 5
  Placement = pos=(0,0,0) rot=(1,0,0;3.14159rad)
  Support = -> [Pad002]
  sketch-geometry (7):
    g0: LineSegment StartX=1.275 StartY=0.736122 StartZ=0 EndX=0 EndY=1.47224 EndZ=0
    g1: LineSegment StartX=0 StartY=1.47224 StartZ=0 EndX=-1.275 EndY=0.736122 EndZ=0
    g2: LineSegment StartX=-1.275 StartY=0.736122 StartZ=0 EndX=-1.275 EndY=-0.736122 EndZ=0
    g3: LineSegment StartX=-1.275 StartY=-0.736122 StartZ=0 EndX=1.34766e-11 EndY=-1.47224 EndZ=0
    g4: LineSegment StartX=1.34766e-11 StartY=-1.47224 StartZ=0 EndX=1.275 EndY=-0.736122 EndZ=0
    g5: LineSegment StartX=1.275 StartY=-0.736122 StartZ=0 EndX=1.275 EndY=0.736122 EndZ=0
    g6: Circle [constr] CenterX=0 CenterY=0 CenterZ=0 NormalX=0 NormalY=0 NormalZ=1 AngleXU=0 Radius=1.47224
  constraints (16):
    c: Coincident(g0,g1)
    c: Coincident(g1,g2)
    c: Coincident(g2,g3)
    c: Coincident(g3,g4)
    c: Coincident(g4,g5)
    c: Coincident(g5,g0)
    c: Equal(g0, g1-g5) x5
    c: PointOnObject(g0,g6)
    c: PointOnObject(g1,g6)
    c: PointOnObject(g2,g6)
    c: PointOnObject(g3,g6)
    c: PointOnObject(g4,g6)
    c: PointOnObject(g5,g6)
    c: Coincident(g6,g-1)
    c: PointOnObject(g0,g-2)
    c: DistanceX(g1,g0) = 2.55
FEATURE [PartDesign::Pocket] Pocket096  label="M3x8 Wrench"
  BaseFeature = -> Pad002
  Length = 1.3
  Length2 = 100
  Profile = -> Sketch131
  Type = 0
FEATURE [PartDesign::Chamfer] Chamfer038  label="M3x8 Smooth"
  Base = -> Pocket096 [Face11,Edge2,Edge24,Edge3]
  BaseFeature = -> Pocket096
  Size = 0.2
FEATURE [Sketcher::SketchObject] Sketch320
  MapMode = 5
  Placement = pos=(0,0,0) rot=(1,0,0;3.14159rad)
  Support = -> [Pad025]
  sketch-geometry (7):
    g0: LineSegment StartX=1.275 StartY=0.736122 StartZ=0 EndX=0 EndY=1.47224 EndZ=0
    g1: LineSegment StartX=0 StartY=1.47224 StartZ=0 EndX=-1.275 EndY=0.736122 EndZ=0
    g2: LineSegment StartX=-1.275 StartY=0.736122 StartZ=0 EndX=-1.275 EndY=-0.736122 EndZ=0
    g3: LineSegment StartX=-1.275 StartY=-0.736122 StartZ=0 EndX=1.34766e-11 EndY=-1.47224 EndZ=0
    g4: LineSegment StartX=1.34766e-11 StartY=-1.47224 StartZ=0 EndX=1.275 EndY=-0.736122 EndZ=0
    g5: LineSegment StartX=1.275 StartY=-0.736122 StartZ=0 EndX=1.275 EndY=0.736122 EndZ=0
    g6: Circle [constr] CenterX=0 CenterY=0 CenterZ=0 NormalX=0 NormalY=0 NormalZ=1 AngleXU=0 Radius=1.47224
  constraints (16):
    c: Coincident(g0,g1)
    c: Coincident(g1,g2)
    c: Coincident(g2,g3)
    c: Coincident(g3,g4)
    c: Coincident(g4,g5)
    c: Coincident(g5,g0)
    c: Equal(g0, g1-g5) x5
    c: PointOnObject(g0,g6)
    c: PointOnObject(g1,g6)
    c: PointOnObject(g2,g6)
    c: PointOnObject(g3,g6)
    c: PointOnObject(g4,g6)
    c: PointOnObject(g5,g6)
    c: Coincident(g6,g-1)
    c: PointOnObject(g0,g-2)
    c: DistanceX(g1,g0) = 2.55
FEATURE [PartDesign::Pocket] Pocket097  label="M3x8 Wrench014"
  BaseFeature = -> Pad025
  Length = 1.3
  Length2 = 100
  Profile = -> Sketch320
  Type = 0
FEATURE [PartDesign::Chamfer] Chamfer039  label="M3x8 Smooth014"
  Base = -> Pocket097 [Face11,Edge2,Edge24,Edge3]
  BaseFeature = -> Pocket097
  Size = 0.2
FEATURE [Sketcher::SketchObject] Sketch145
  MapMode = 5
  Support = -> [XY_Plane017]
  sketch-geometry (1):
    g0: Circle CenterX=0 CenterY=0 CenterZ=0 NormalX=0 NormalY=0 NormalZ=1 AngleXU=0 Radius=1.9
  constraints (2):
    c: Coincident(g0,g-1)
    c: Radius(g0) = 1.9
FEATURE [PartDesign::Pad] Pad097  label="M3x8 Head013"
  Length = 2
  Length2 = 100
  Profile = -> Sketch145
  Type = 0
FEATURE [Sketcher::SketchObject] Sketch321
  MapMode = 5
  Support = -> [XY_Plane016]
  sketch-geometry (8):
    g0: LineSegment StartX=0 StartY=2.3094 StartZ=0 EndX=-2 EndY=1.1547 EndZ=0
    g1: LineSegment StartX=-2 StartY=1.1547 StartZ=0 EndX=-2 EndY=-1.1547 EndZ=0
    g2: LineSegment StartX=-2 StartY=-1.1547 StartZ=0 EndX=-2e-16 EndY=-2.3094 EndZ=0
    g3: LineSegment StartX=-2e-16 StartY=-2.3094 StartZ=0 EndX=2 EndY=-1.1547 EndZ=0
    g4: LineSegment StartX=2 StartY=-1.1547 StartZ=0 EndX=2 EndY=1.1547 EndZ=0
    g5: LineSegment StartX=2 StartY=1.1547 StartZ=0 EndX=0 EndY=2.3094 EndZ=0
    g6: Circle [constr] CenterX=0 CenterY=0 CenterZ=0 NormalX=0 NormalY=0 NormalZ=1 AngleXU=0 Radius=2.3094
    g7: Circle CenterX=0 CenterY=0 CenterZ=0 NormalX=0 NormalY=0 NormalZ=1 AngleXU=0 Radius=1
  constraints (18):
    c: Coincident(g0,g1)
    c: Coincident(g1,g2)
    c: Coincident(g2,g3)
    c: Coincident(g3,g4)
    c: Coincident(g4,g5)
    c: Coincident(g5,g0)
    c: Equal(g0, g1-g5) x5
    c: PointOnObject(g0,g6)
    c: PointOnObject(g1,g6)
    c: PointOnObject(g2,g6)
    c: PointOnObject(g3,g6)
    c: PointOnObject(g4,g6)
    c: PointOnObject(g5,g6)
    c: Coincident(g6,g-1)
    c: PointOnObject(g5,g-2)
    c: DistanceX(g0,g4) = 4
    c: Coincident(g7,g-1)
    c: Radius(g7) = 1
FEATURE [PartDesign::Pad] Pad095  label="M3 Nut Primitive013"
  Length = 0.6
  Length2 = 0.6
  Profile = -> Sketch321
  Type = 4
FEATURE [Sketcher::SketchObject] Sketch322
  ExternalGeometry = -> [Pad095]
  MapMode = 5
  Placement = pos=(0,0,0) rot=(0.57735,0.57735,0.57735;2.0944rad)
  Support = -> [YZ_Plane016]
  sketch-geometry (6):
    g0: LineSegment StartX=-1.9594 StartY=0.6 StartZ=0 EndX=-2.8094 EndY=0.6 EndZ=0
    g1: LineSegment StartX=-2.8094 StartY=0.6 StartZ=0 EndX=-2.8094 EndY=-0.6 EndZ=0
    g2: LineSegment StartX=-2.8094 StartY=-0.6 StartZ=0 EndX=-1.9594 EndY=-0.6 EndZ=0
    g3: LineSegment StartX=-1.9594 StartY=-0.6 StartZ=0 EndX=-2.3094 EndY=-0.4 EndZ=0
    g4: LineSegment StartX=-2.3094 StartY=-0.4 StartZ=0 EndX=-2.3094 EndY=0.4 EndZ=0
    g5: LineSegment StartX=-2.3094 StartY=0.4 StartZ=0 EndX=-1.9594 EndY=0.6 EndZ=0
  constraints (15):
    c: Horizontal(g0)
    c: Coincident(g0,g1)
    c: Coincident(g1,g2)
    c: Coincident(g2,g3)
    c: Coincident(g3,g4)
    c: Coincident(g4,g5)
    c: Coincident(g5,g0)
    c: Symmetric(g4,g3,g-1)
    c: Symmetric(g0,g2,g-1)
    c: Symmetric(g1,g0,g-1)
    c: DistanceX(g0,g4) = 0.5
    c: DistanceY(g3,g4) = 0.8
    c: DistanceY(g1,g0) = 1.2
    c: PointOnObject(g3,g-3)
    c: DistanceX(g4,g0) = 0.35
FEATURE [PartDesign::Groove] Groove013  label="M3 Nut Smooth013"
  Angle = 360
  Axis = (-2e-16,3e-16,1)
  Base = (0,0,0)
  BaseFeature = -> Pad095
  Profile = -> Sketch322
  ReferenceAxis = -> Sketch322 [V_Axis]
  Reversed = true
FEATURE [PartDesign::Chamfer] Chamfer037  label="M3 Nut Smooth Hole017"
  Base = -> Groove013 [Edge24,Edge23]
  BaseFeature = -> Groove013
  Size = 0.2
FEATURE [Sketcher::SketchObject] Sketch142
  MapMode = 5
  Support = -> [XY_Plane015]
  sketch-geometry (4):
    g0: LineSegment StartX=0 StartY=0 StartZ=0 EndX=56.5 EndY=0 EndZ=0
    g1: LineSegment StartX=56.5 StartY=0 StartZ=0 EndX=56.5 EndY=-22 EndZ=0
    g2: LineSegment StartX=56.5 StartY=-22 StartZ=0 EndX=0 EndY=-22 EndZ=0
    g3: LineSegment StartX=0 StartY=-22 StartZ=0 EndX=0 EndY=0 EndZ=0
  constraints (11):
    c: Coincident(g0,g1)
    c: Coincident(g1,g2)
    c: Coincident(g2,g3)
    c: Coincident(g3,g0)
    c: Horizontal(g0)
    c: Horizontal(g2)
    c: Vertical(g1)
    c: Vertical(g3)
    c: Coincident(g0,g-1)
    c: DistanceX(g2,g2) = 56.5
    c: DistanceY(g3,g3) = 22
FEATURE [PartDesign::Pad] Pad028  label="Baseplate004"
  Length = 25
  Length2 = 100
  Profile = -> Sketch142
  Type = 0
FEATURE [Sketcher::SketchObject] Sketch139
  MapMode = 5
  Placement = pos=(0,0,25) rot=(0,0,1;0rad)
  Support = -> [Pad028]
  sketch-geometry (4):
    g0: LineSegment StartX=8 StartY=0 StartZ=0 EndX=48.5 EndY=0 EndZ=0
    g1: LineSegment StartX=48.5 StartY=0 StartZ=0 EndX=48.5 EndY=-19 EndZ=0
    g2: LineSegment StartX=48.5 StartY=-19 StartZ=0 EndX=8 EndY=-19 EndZ=0
    g3: LineSegment StartX=8 StartY=-19 StartZ=0 EndX=8 EndY=0 EndZ=0
  constraints (12):
    c: Coincident(g0,g1)
    c: Coincident(g1,g2)
    c: Coincident(g2,g3)
    c: Coincident(g3,g0)
    c: Horizontal(g0)
    c: Horizontal(g2)
    c: Vertical(g1)
    c: Vertical(g3)
    c: PointOnObject(g0,g-1)
    c: DistanceY(g3,g3) = 19
    c: DistanceX(g0,g0) = 40.5
    c: DistanceX(g-1,g0) = 8
FEATURE [PartDesign::Pocket] Pocket098  label="Servopocket"
  BaseFeature = -> Pad028
  Length = 20
  Length2 = 100
  Profile = -> Sketch139
  Type = 0
FEATURE [Sketcher::SketchObject] Sketch143
  MapMode = 5
  Placement = pos=(0,0,25) rot=(0,0,1;0rad)
  Support = -> [Pocket098]
  sketch-geometry (5):
    g0: ArcOfCircle CenterX=22.5 CenterY=23.1875 CenterZ=0 NormalX=0 NormalY=0 NormalZ=1 AngleXU=0 Radius=45.1875 StartAngle=4.19118 EndAngle=4.71239
    g1: LineSegment StartX=22.5 StartY=-22 StartZ=0 EndX=56.5 EndY=-22 EndZ=0
    g2: LineSegment StartX=56.5 StartY=-22 StartZ=0 EndX=56.5 EndY=-23 EndZ=0
    g3: LineSegment StartX=56.5 StartY=-23 StartZ=0 EndX=0 EndY=-23 EndZ=0
    g4: LineSegment StartX=0 StartY=-23 StartZ=0 EndX=0 EndY=-16 EndZ=0
  constraints (15):
    c: PointOnObject(g0,g-2)
    c: Horizontal(g1)
    c: Coincident(g2,g1)
    c: Vertical(g2)
    c: Coincident(g3,g2)
    c: Horizontal(g3)
    c: Coincident(g4,g3)
    c: Coincident(g4,g0)
    c: Vertical(g4)
    c: Tangent(g1,g0) = -1.5708
    c: DistanceX(g0,g0) = 22.5
    c: DistanceY(g4,g4) = 7
    c: DistanceY(g2,g2) = 1
    c: DistanceY(g0,g-1) = 16
    c: DistanceX(g3,g3) = 56.5
FEATURE [PartDesign::Pocket] Pocket100  label="Swing Counterpart"
  BaseFeature = -> Pocket098
  Length = 25
  Length2 = 100
  Profile = -> Sketch143
  Type = 0
FEATURE [Sketcher::SketchObject] Sketch324
  MapMode = 5
  Placement = pos=(56.5,0,0) rot=(0.57735,0.57735,0.57735;2.0944rad)
  Support = -> [Pocket100]
  sketch-geometry (8):
    g0: LineSegment StartX=-6 StartY=22.9 StartZ=0 EndX=-3 EndY=22.9 EndZ=0
    g1: LineSegment StartX=-3 StartY=22.9 StartZ=0 EndX=-3 EndY=17.1 EndZ=0
    g2: LineSegment StartX=-3 StartY=17.1 StartZ=0 EndX=-6 EndY=17.1 EndZ=0
    g3: LineSegment StartX=-6 StartY=17.1 StartZ=0 EndX=-6 EndY=22.9 EndZ=0
    g4: LineSegment StartX=-6 StartY=12.9 StartZ=0 EndX=-3 EndY=12.9 EndZ=0
    g5: LineSegment StartX=-3 StartY=12.9 StartZ=0 EndX=-3 EndY=7.1 EndZ=0
    g6: LineSegment StartX=-3 StartY=7.1 StartZ=0 EndX=-6 EndY=7.1 EndZ=0
    g7: LineSegment StartX=-6 StartY=7.1 StartZ=0 EndX=-6 EndY=12.9 EndZ=0
  constraints (24):
    c: Coincident(g0,g1)
    c: Coincident(g1,g2)
    c: Coincident(g2,g3)
    c: Coincident(g3,g0)
    c: Horizontal(g0)
    c: Horizontal(g2)
    c: Vertical(g1)
    c: Vertical(g3)
    c: Coincident(g4,g5)
    c: Coincident(g5,g6)
    c: Coincident(g6,g7)
    c: Coincident(g7,g4)
    c: Horizontal(g4)
    c: Horizontal(g6)
    c: Vertical(g5)
    c: Vertical(g7)
    c: Equal(g1,g5)
    c: Equal(g4,g2)
    c: Vertical(g1,g4)
    c: DistanceX(g0,g0) = 3
    c: DistanceY(g1,g1) = 5.8
    c: DistanceY(g5,g1) = 10
    c: DistanceY(g-1,g5) = 7.1
    c: DistanceX(g5,g-1) = 3
FEATURE [PartDesign::Pocket] Pocket102  label="Nutholes"
  BaseFeature = -> Pocket100
  Length = 56.5
  Length2 = 100
  Profile = -> Sketch324
  Type = 0
FEATURE [Sketcher::SketchObject] Sketch138
  MapMode = 5
  Placement = pos=(0,0,0) rot=(0,0.707107,0.707107;3.14159rad)
  Support = -> [Pocket102]
  sketch-geometry (4):
    g0: Circle CenterX=-52.5 CenterY=20 CenterZ=0 NormalX=0 NormalY=0 NormalZ=1 AngleXU=0 Radius=1.6
    g1: Circle CenterX=-52.5 CenterY=10 CenterZ=0 NormalX=0 NormalY=0 NormalZ=1 AngleXU=0 Radius=1.6
    g2: Circle CenterX=-4 CenterY=20 CenterZ=0 NormalX=0 NormalY=0 NormalZ=1 AngleXU=0 Radius=1.6
    g3: Circle CenterX=-4 CenterY=10 CenterZ=0 NormalX=0 NormalY=0 NormalZ=1 AngleXU=0 Radius=1.6
  constraints (12):
    c: Horizontal(g2,g0)
    c: Horizontal(g1,g3)
    c: Vertical(g3,g2)
    c: Vertical(g0,g1)
    c: Equal(g0,g1)
    c: Equal(g1,g2)
    c: Equal(g2,g3)
    c: Radius(g2) = 1.6
    c: DistanceX(g0,g2) = 48.5
    c: DistanceY(g3,g2) = 10
    c: DistanceY(g-1,g3) = 10
    c: DistanceX(g3,g-1) = 4
FEATURE [PartDesign::Pocket] Pocket099  label="Screwholes001"
  BaseFeature = -> Pocket102
  Length = 8.5
  Length2 = 100
  Profile = -> Sketch138
  Type = 0
FEATURE [Sketcher::SketchObject] Sketch140
  MapMode = 5
  Placement = pos=(56.5,0,0) rot=(0.57735,0.57735,0.57735;2.0944rad)
  Support = -> [Pocket099]
  sketch-geometry (4):
    g0: ArcOfCircle CenterX=-12 CenterY=11.5 CenterZ=0 NormalX=0 NormalY=0 NormalZ=1 AngleXU=0 Radius=2.5 StartAngle=3.14159 EndAngle=6.28319
    g1: LineSegment StartX=-14.5 StartY=11.5 StartZ=0 EndX=-14.5 EndY=25 EndZ=0
    g2: LineSegment StartX=-14.5 StartY=25 StartZ=0 EndX=-9.5 EndY=25 EndZ=0
    g3: LineSegment StartX=-9.5 StartY=25 StartZ=0 EndX=-9.5 EndY=11.5 EndZ=0
  constraints (13):
    c: Horizontal(g0,g0)
    c: Horizontal(g0,g0)
    c: Coincident(g1,g0)
    c: Vertical(g1)
    c: Coincident(g2,g1)
    c: Horizontal(g2)
    c: Coincident(g3,g2)
    c: Coincident(g3,g0)
    c: Vertical(g3)
    c: Radius(g0) = 2.5
    c: DistanceX(g0,g-1) = 12
    c: DistanceY(g-1,g0) = 11.5
    c: DistanceY(g-1,g2) = 25
FEATURE [PartDesign::Pocket] Pocket104  label="Servocable Pocket"
  BaseFeature = -> Pocket099
  Length = 8
  Length2 = 100
  Profile = -> Sketch140
  Type = 0
FEATURE [PartDesign::Fillet] Fillet035  label="Servocable Smooth Edges"
  Base = -> Pocket104 [Edge48,Edge43]
  BaseFeature = -> Pocket104
  Radius = 0.5
FEATURE [Sketcher::SketchObject] Sketch323
  MapMode = 5
  Placement = pos=(0,-22,0) rot=(1,0,0;1.5708rad)
  Support = -> [Fillet035]
  sketch-geometry (1):
    g0: Circle CenterX=38.25 CenterY=15 CenterZ=0 NormalX=0 NormalY=0 NormalZ=1 AngleXU=0 Radius=0.95
  constraints (3):
    c: DistanceY(g-1,g0) = 15
    c: DistanceX(g-1,g0) = 38.25
    c: Radius(g0) = 0.95
FEATURE [PartDesign::Pocket] Pocket101  label="Ball Bearing Pin Screwhole"
  BaseFeature = -> Fillet035
  Length = 3
  Length2 = 100
  Profile = -> Sketch323
  Type = 0
FEATURE [Sketcher::SketchObject] Sketch144
  ExternalGeometry = -> [Pocket101]
  MapMode = 5
  Placement = pos=(0,-19,0) rot=(0,0.707107,0.707107;3.14159rad)
  Support = -> [Pocket101]
  sketch-geometry (7):
    g0: LineSegment StartX=-36.2 StartY=16.1836 StartZ=0 EndX=-38.25 EndY=17.3671 EndZ=0
    g1: LineSegment StartX=-38.25 StartY=17.3671 StartZ=0 EndX=-40.3 EndY=16.1836 EndZ=0
    g2: LineSegment StartX=-40.3 StartY=16.1836 StartZ=0 EndX=-40.3 EndY=13.8164 EndZ=0
    g3: LineSegment StartX=-40.3 StartY=13.8164 StartZ=0 EndX=-38.25 EndY=12.6329 EndZ=0
    g4: LineSegment StartX=-38.25 StartY=12.6329 StartZ=0 EndX=-36.2 EndY=13.8164 EndZ=0
    g5: LineSegment StartX=-36.2 StartY=13.8164 StartZ=0 EndX=-36.2 EndY=16.1836 EndZ=0
    g6: Circle [constr] CenterX=-38.25 CenterY=15 CenterZ=0 NormalX=0 NormalY=0 NormalZ=1 AngleXU=0 Radius=2.36714
  constraints (16):
    c: Coincident(g0,g1)
    c: Coincident(g1,g2)
    c: Coincident(g2,g3)
    c: Coincident(g3,g4)
    c: Coincident(g4,g5)
    c: Coincident(g5,g0)
    c: Equal(g0, g1-g5) x5
    c: PointOnObject(g0,g6)
    c: PointOnObject(g1,g6)
    c: PointOnObject(g2,g6)
    c: PointOnObject(g3,g6)
    c: PointOnObject(g4,g6)
    c: PointOnObject(g5,g6)
    c: Coincident(g6,g-3)
    c: Vertical(g5)
    c: DistanceX(g1,g0) = 4.1
FEATURE [PartDesign::Pocket] Pocket103  label="Ball Bearing Pin Nuthole"
  BaseFeature = -> Pocket101
  Length = 1.5
  Length2 = 100
  Profile = -> Sketch144
  Type = 0
FEATURE [PartDesign::Fillet] Fillet036  label="Smooth Counterpart Corner"
  Base = -> Pocket103 [Edge3]
  BaseFeature = -> Pocket103
  Radius = 5
FEATURE [PartDesign::Fillet] Fillet037  label="Smooth Servo Pocket"
  Base = -> Fillet036 [Edge80,Edge77,Edge76,Edge79,Edge95]
  BaseFeature = -> Fillet036
  Radius = 1
FEATURE [Sketcher::SketchObject] Sketch141
  MapMode = 5
  Placement = pos=(0,0,0) rot=(0,0.707107,0.707107;3.14159rad)
  Support = -> [Fillet037]
  sketch-geometry (4):
    g0: LineSegment StartX=0 StartY=0 StartZ=0 EndX=-56.5 EndY=0 EndZ=0
    g1: LineSegment StartX=-56.5 StartY=0 StartZ=0 EndX=-56.5 EndY=5 EndZ=0
    g2: LineSegment StartX=-56.5 StartY=5 StartZ=0 EndX=0 EndY=5 EndZ=0
    g3: LineSegment StartX=0 StartY=5 StartZ=0 EndX=0 EndY=0 EndZ=0
  constraints (11):
    c: Coincident(g0,g1)
    c: Coincident(g1,g2)
    c: Coincident(g2,g3)
    c: Coincident(g3,g0)
    c: Horizontal(g0)
    c: Horizontal(g2)
    c: Vertical(g1)
    c: Vertical(g3)
    c: Coincident(g0,g-1)
    c: DistanceY(g1,g1) = 5
    c: DistanceX(g2,g2) = 56.5
FEATURE [PartDesign::Pad] Pad027  label="Elongate Baseplate"
  BaseFeature = -> Fillet037
  Length = 10
  Length2 = 100
  Profile = -> Sketch141
  Type = 0
FEATURE [PartDesign::Fillet] Fillet038  label="Smooth Edges003"
  Base = -> Pad027 [Edge135,Edge159]
  BaseFeature = -> Pad027
  Radius = 0.4
FEATURE [Sketcher::SketchObject] Sketch325
  MapMode = 5
  Placement = pos=(0,0,2) rot=(0,0,1;0rad)
  Support = -> [Pad097]
  sketch-geometry (1):
    g0: Circle CenterX=0 CenterY=0 CenterZ=0 NormalX=0 NormalY=0 NormalZ=1 AngleXU=0 Radius=1
  constraints (2):
    c: Coincident(g0,g-1)
    c: Radius(g0) = 1
FEATURE [PartDesign::Pad] Pad096  label="M3x8 Thread013"
  BaseFeature = -> Pad097
  Length = 8
  Length2 = 100
  Profile = -> Sketch325
  Type = 0
FEATURE [Sketcher::SketchObject] Sketch146
  MapMode = 5
  Placement = pos=(0,0,0) rot=(1,0,0;3.14159rad)
  Support = -> [Pad096]
  sketch-geometry (7):
    g0: LineSegment StartX=0.77 StartY=0.44456 StartZ=0 EndX=0 EndY=0.889119 EndZ=0
    g1: LineSegment StartX=0 StartY=0.889119 StartZ=0 EndX=-0.77 EndY=0.44456 EndZ=0
    g2: LineSegment StartX=-0.77 StartY=0.44456 StartZ=0 EndX=-0.77 EndY=-0.44456 EndZ=0
    g3: LineSegment StartX=-0.77 StartY=-0.44456 StartZ=0 EndX=3.85628e-11 EndY=-0.889119 EndZ=0
    g4: LineSegment StartX=3.85628e-11 StartY=-0.889119 StartZ=0 EndX=0.77 EndY=-0.44456 EndZ=0
    g5: LineSegment StartX=0.77 StartY=-0.44456 StartZ=0 EndX=0.77 EndY=0.44456 EndZ=0
    g6: Circle [constr] CenterX=0 CenterY=0 CenterZ=0 NormalX=0 NormalY=0 NormalZ=1 AngleXU=0 Radius=0.889119
  constraints (16):
    c: Coincident(g0,g1)
    c: Coincident(g1,g2)
    c: Coincident(g2,g3)
    c: Coincident(g3,g4)
    c: Coincident(g4,g5)
    c: Coincident(g5,g0)
    c: Equal(g0, g1-g5) x5
    c: PointOnObject(g0,g6)
    c: PointOnObject(g1,g6)
    c: PointOnObject(g2,g6)
    c: PointOnObject(g3,g6)
    c: PointOnObject(g4,g6)
    c: PointOnObject(g5,g6)
    c: Coincident(g6,g-1)
    c: PointOnObject(g0,g-2)
    c: DistanceX(g1,g0) = 1.54
FEATURE [PartDesign::Pocket] Pocket105  label="M3x8 Wrench013"
  BaseFeature = -> Pad096
  Length = 1
  Length2 = 100
  Profile = -> Sketch146
  Type = 0
FEATURE [PartDesign::Chamfer] Chamfer029  label="M3x8 Smooth013"
  Base = -> Pocket105 [Face11,Edge2,Edge24,Edge3]
  BaseFeature = -> Pocket105
  Size = 0.2
FEATURE [Sketcher::SketchObject] Sketch161
  MapMode = 5
  Support = -> [XY_Plane022]
  sketch-geometry (8):
    g0: LineSegment StartX=0 StartY=3.17543 StartZ=0 EndX=-2.75 EndY=1.58771 EndZ=0
    g1: LineSegment StartX=-2.75 StartY=1.58771 StartZ=0 EndX=-2.75 EndY=-1.58771 EndZ=0
    g2: LineSegment StartX=-2.75 StartY=-1.58771 StartZ=0 EndX=0 EndY=-3.17543 EndZ=0
    g3: LineSegment StartX=0 StartY=-3.17543 StartZ=0 EndX=2.75 EndY=-1.58771 EndZ=0
    g4: LineSegment StartX=2.75 StartY=-1.58771 StartZ=0 EndX=2.75 EndY=1.58771 EndZ=0
    g5: LineSegment StartX=2.75 StartY=1.58771 StartZ=0 EndX=0 EndY=3.17543 EndZ=0
    g6: Circle [constr] CenterX=0 CenterY=0 CenterZ=0 NormalX=0 NormalY=0 NormalZ=1 AngleXU=0 Radius=3.17543
    g7: Circle CenterX=0 CenterY=0 CenterZ=0 NormalX=0 NormalY=0 NormalZ=1 AngleXU=0 Radius=1.5
  constraints (18):
    c: Coincident(g0,g1)
    c: Coincident(g1,g2)
    c: Coincident(g2,g3)
    c: Coincident(g3,g4)
    c: Coincident(g4,g5)
    c: Coincident(g5,g0)
    c: Equal(g0, g1-g5) x5
    c: PointOnObject(g0,g6)
    c: PointOnObject(g1,g6)
    c: PointOnObject(g2,g6)
    c: PointOnObject(g3,g6)
    c: PointOnObject(g4,g6)
    c: PointOnObject(g5,g6)
    c: Coincident(g6,g-1)
    c: PointOnObject(g5,g-2)
    c: DistanceX(g0,g4) = 5.5
    c: Coincident(g7,g-1)
    c: Radius(g7) = 1.5
FEATURE [PartDesign::Pad] Pad036  label="M3 Nut Primitive014"
  Length = 1.2
  Length2 = 1.2
  Profile = -> Sketch161
  Type = 4
FEATURE [Sketcher::SketchObject] Sketch162
  ExternalGeometry = -> [Pad036]
  MapMode = 5
  Placement = pos=(0,0,0) rot=(0.57735,0.57735,0.57735;2.0944rad)
  Support = -> [YZ_Plane022]
  sketch-geometry (6):
    g0: LineSegment StartX=-2.67543 StartY=1.2 StartZ=0 EndX=-3.67543 EndY=1.2 EndZ=0
    g1: LineSegment StartX=-3.67543 StartY=1.2 StartZ=0 EndX=-3.67543 EndY=-1.2 EndZ=0
    g2: LineSegment StartX=-3.67543 StartY=-1.2 StartZ=0 EndX=-2.67543 EndY=-1.2 EndZ=0
    g3: LineSegment StartX=-2.67543 StartY=-1.2 StartZ=0 EndX=-3.17543 EndY=-1 EndZ=0
    g4: LineSegment StartX=-3.17543 StartY=-1 StartZ=0 EndX=-3.17543 EndY=1 EndZ=0
    g5: LineSegment StartX=-3.17543 StartY=1 StartZ=0 EndX=-2.67543 EndY=1.2 EndZ=0
  constraints (15):
    c: Horizontal(g0)
    c: Coincident(g0,g1)
    c: Coincident(g1,g2)
    c: Coincident(g2,g3)
    c: Coincident(g3,g4)
    c: Coincident(g4,g5)
    c: Coincident(g5,g0)
    c: Symmetric(g4,g3,g-1)
    c: Symmetric(g0,g2,g-1)
    c: Symmetric(g1,g0,g-1)
    c: DistanceX(g0,g4) = 0.5
    c: DistanceY(g3,g4) = 2
    c: DistanceY(g1,g0) = 2.4
    c: PointOnObject(g3,g-3)
    c: DistanceX(g4,g0) = 0.5
FEATURE [PartDesign::Groove] Groove014  label="M3 Nut Smooth014"
  Angle = 360
  Axis = (-2e-16,3e-16,1)
  Base = (0,0,0)
  BaseFeature = -> Pad036
  Profile = -> Sketch162
  ReferenceAxis = -> Sketch162 [V_Axis]
  Reversed = true
FEATURE [PartDesign::Chamfer] Chamfer035  label="M3 Nut Smooth Hole015"
  Base = -> Groove014 [Edge24,Edge23]
  BaseFeature = -> Groove014
  Size = 0.2
FEATURE [Sketcher::SketchObject] Sketch163
  MapMode = 5
  Support = -> [XY_Plane023]
  sketch-geometry (8):
    g0: LineSegment StartX=0 StartY=3.17543 StartZ=0 EndX=-2.75 EndY=1.58771 EndZ=0
    g1: LineSegment StartX=-2.75 StartY=1.58771 StartZ=0 EndX=-2.75 EndY=-1.58771 EndZ=0
    g2: LineSegment StartX=-2.75 StartY=-1.58771 StartZ=0 EndX=0 EndY=-3.17543 EndZ=0
    g3: LineSegment StartX=0 StartY=-3.17543 StartZ=0 EndX=2.75 EndY=-1.58771 EndZ=0
    g4: LineSegment StartX=2.75 StartY=-1.58771 StartZ=0 EndX=2.75 EndY=1.58771 EndZ=0
    g5: LineSegment StartX=2.75 StartY=1.58771 StartZ=0 EndX=0 EndY=3.17543 EndZ=0
    g6: Circle [constr] CenterX=0 CenterY=0 CenterZ=0 NormalX=0 NormalY=0 NormalZ=1 AngleXU=0 Radius=3.17543
    g7: Circle CenterX=0 CenterY=0 CenterZ=0 NormalX=0 NormalY=0 NormalZ=1 AngleXU=0 Radius=1.5
  constraints (18):
    c: Coincident(g0,g1)
    c: Coincident(g1,g2)
    c: Coincident(g2,g3)
    c: Coincident(g3,g4)
    c: Coincident(g4,g5)
    c: Coincident(g5,g0)
    c: Equal(g0, g1-g5) x5
    c: PointOnObject(g0,g6)
    c: PointOnObject(g1,g6)
    c: PointOnObject(g2,g6)
    c: PointOnObject(g3,g6)
    c: PointOnObject(g4,g6)
    c: PointOnObject(g5,g6)
    c: Coincident(g6,g-1)
    c: PointOnObject(g5,g-2)
    c: DistanceX(g0,g4) = 5.5
    c: Coincident(g7,g-1)
    c: Radius(g7) = 1.5
FEATURE [PartDesign::Pad] Pad037  label="M3 Nut Primitive015"
  Length = 1.2
  Length2 = 1.2
  Profile = -> Sketch163
  Type = 4
FEATURE [Sketcher::SketchObject] Sketch147
  MapMode = 5
  Support = -> [XY_Plane018]
  sketch-geometry (2):
    g0: Circle CenterX=0 CenterY=0 CenterZ=0 NormalX=0 NormalY=0 NormalZ=1 AngleXU=0 Radius=2.5
    g1: Circle CenterX=0 CenterY=0 CenterZ=0 NormalX=0 NormalY=0 NormalZ=1 AngleXU=0 Radius=1
  constraints (4):
    c: Coincident(g0,g-1)
    c: Coincident(g1,g0)
    c: Radius(g0) = 2.5
    c: Radius(g1) = 1
FEATURE [PartDesign::Pad] Pad029  label="Ball Bearing Pin"
  Length = 5
  Length2 = 100
  Profile = -> Sketch147
  Type = 0
FEATURE [PartDesign::Chamfer] Chamfer027  label="Smooth Pinhead"
  Base = -> Pad029 [Edge3]
  BaseFeature = -> Pad029
  Size = 0.4
FEATURE [Sketcher::SketchObject] Sketch164
  ExternalGeometry = -> [Pad037]
  MapMode = 5
  Placement = pos=(0,0,0) rot=(0.57735,0.57735,0.57735;2.0944rad)
  Support = -> [YZ_Plane023]
  sketch-geometry (6):
    g0: LineSegment StartX=-2.67543 StartY=1.2 StartZ=0 EndX=-3.67543 EndY=1.2 EndZ=0
    g1: LineSegment StartX=-3.67543 StartY=1.2 StartZ=0 EndX=-3.67543 EndY=-1.2 EndZ=0
    g2: LineSegment StartX=-3.67543 StartY=-1.2 StartZ=0 EndX=-2.67543 EndY=-1.2 EndZ=0
    g3: LineSegment StartX=-2.67543 StartY=-1.2 StartZ=0 EndX=-3.17543 EndY=-1 EndZ=0
    g4: LineSegment StartX=-3.17543 StartY=-1 StartZ=0 EndX=-3.17543 EndY=1 EndZ=0
    g5: LineSegment StartX=-3.17543 StartY=1 StartZ=0 EndX=-2.67543 EndY=1.2 EndZ=0
  constraints (15):
    c: Horizontal(g0)
    c: Coincident(g0,g1)
    c: Coincident(g1,g2)
    c: Coincident(g2,g3)
    c: Coincident(g3,g4)
    c: Coincident(g4,g5)
    c: Coincident(g5,g0)
    c: Symmetric(g4,g3,g-1)
    c: Symmetric(g0,g2,g-1)
    c: Symmetric(g1,g0,g-1)
    c: DistanceX(g0,g4) = 0.5
    c: DistanceY(g3,g4) = 2
    c: DistanceY(g1,g0) = 2.4
    c: PointOnObject(g3,g-3)
    c: DistanceX(g4,g0) = 0.5
FEATURE [PartDesign::Groove] Groove016  label="M3 Nut Smooth015"
  Angle = 360
  Axis = (-2e-16,3e-16,1)
  Base = (0,0,0)
  BaseFeature = -> Pad037
  Profile = -> Sketch164
  ReferenceAxis = -> Sketch164 [V_Axis]
  Reversed = true
FEATURE [PartDesign::Chamfer] Chamfer036  label="M3 Nut Smooth Hole016"
  Base = -> Groove016 [Edge24,Edge23]
  BaseFeature = -> Groove016
  Size = 0.2
FEATURE [Sketcher::SketchObject] Sketch165
  MapMode = 5
  Support = -> [XY_Plane024]
  sketch-geometry (8):
    g0: LineSegment StartX=0 StartY=3.17543 StartZ=0 EndX=-2.75 EndY=1.58771 EndZ=0
    g1: LineSegment StartX=-2.75 StartY=1.58771 StartZ=0 EndX=-2.75 EndY=-1.58771 EndZ=0
    g2: LineSegment StartX=-2.75 StartY=-1.58771 StartZ=0 EndX=0 EndY=-3.17543 EndZ=0
    g3: LineSegment StartX=0 StartY=-3.17543 StartZ=0 EndX=2.75 EndY=-1.58771 EndZ=0
    g4: LineSegment StartX=2.75 StartY=-1.58771 StartZ=0 EndX=2.75 EndY=1.58771 EndZ=0
    g5: LineSegment StartX=2.75 StartY=1.58771 StartZ=0 EndX=0 EndY=3.17543 EndZ=0
    g6: Circle [constr] CenterX=0 CenterY=0 CenterZ=0 NormalX=0 NormalY=0 NormalZ=1 AngleXU=0 Radius=3.17543
    g7: Circle CenterX=0 CenterY=0 CenterZ=0 NormalX=0 NormalY=0 NormalZ=1 AngleXU=0 Radius=1.5
  constraints (18):
    c: Coincident(g0,g1)
    c: Coincident(g1,g2)
    c: Coincident(g2,g3)
    c: Coincident(g3,g4)
    c: Coincident(g4,g5)
    c: Coincident(g5,g0)
    c: Equal(g0, g1-g5) x5
    c: PointOnObject(g0,g6)
    c: PointOnObject(g1,g6)
    c: PointOnObject(g2,g6)
    c: PointOnObject(g3,g6)
    c: PointOnObject(g4,g6)
    c: PointOnObject(g5,g6)
    c: Coincident(g6,g-1)
    c: PointOnObject(g5,g-2)
    c: DistanceX(g0,g4) = 5.5
    c: Coincident(g7,g-1)
    c: Radius(g7) = 1.5
FEATURE [PartDesign::Pad] Pad038  label="M3 Nut Primitive017"
  Length = 1.2
  Length2 = 1.2
  Profile = -> Sketch165
  Type = 4
FEATURE [Sketcher::SketchObject] Sketch166
  ExternalGeometry = -> [Pad038]
  MapMode = 5
  Placement = pos=(0,0,0) rot=(0.57735,0.57735,0.57735;2.0944rad)
  Support = -> [YZ_Plane024]
  sketch-geometry (6):
    g0: LineSegment StartX=-2.67543 StartY=1.2 StartZ=0 EndX=-3.67543 EndY=1.2 EndZ=0
    g1: LineSegment StartX=-3.67543 StartY=1.2 StartZ=0 EndX=-3.67543 EndY=-1.2 EndZ=0
    g2: LineSegment StartX=-3.67543 StartY=-1.2 StartZ=0 EndX=-2.67543 EndY=-1.2 EndZ=0
    g3: LineSegment StartX=-2.67543 StartY=-1.2 StartZ=0 EndX=-3.17543 EndY=-1 EndZ=0
    g4: LineSegment StartX=-3.17543 StartY=-1 StartZ=0 EndX=-3.17543 EndY=1 EndZ=0
    g5: LineSegment StartX=-3.17543 StartY=1 StartZ=0 EndX=-2.67543 EndY=1.2 EndZ=0
  constraints (15):
    c: Horizontal(g0)
    c: Coincident(g0,g1)
    c: Coincident(g1,g2)
    c: Coincident(g2,g3)
    c: Coincident(g3,g4)
    c: Coincident(g4,g5)
    c: Coincident(g5,g0)
    c: Symmetric(g4,g3,g-1)
    c: Symmetric(g0,g2,g-1)
    c: Symmetric(g1,g0,g-1)
    c: DistanceX(g0,g4) = 0.5
    c: DistanceY(g3,g4) = 2
    c: DistanceY(g1,g0) = 2.4
    c: PointOnObject(g3,g-3)
    c: DistanceX(g4,g0) = 0.5
FEATURE [PartDesign::Groove] Groove017  label="M3 Nut Smooth016"
  Angle = 360
  Axis = (-2e-16,3e-16,1)
  Base = (0,0,0)
  BaseFeature = -> Pad038
  Profile = -> Sketch166
  ReferenceAxis = -> Sketch166 [V_Axis]
  Reversed = true
FEATURE [PartDesign::Chamfer] Chamfer028  label="M3 Nut Smooth Hole013"
  Base = -> Groove017 [Edge24,Edge23]
  BaseFeature = -> Groove017
  Size = 0.2
FEATURE [PartDesign::Body] Body009  label="M3x8"
  Group = -> [Sketch130,Pad001,Sketch132,Pad002,Sketch131,Pocket096,Chamfer038]
  Origin = -> Origin011
  Placement = pos=(0.75,-14,34.25) rot=(-1,0,0;1.5708rad)
  Tip = -> Chamfer038
FEATURE [PartDesign::Body] Body052  label="M2x020"
  Group = -> [Sketch145,Pad097,Sketch325,Pad096,Sketch146,Pocket105,Chamfer029]
  Origin = -> Origin017
  Placement = pos=(-132.394,-126,71.585) rot=(1,0,0;1.5708rad)
  Tip = -> Chamfer029
FEATURE [PartDesign::Body] Body018  label="M3 Nut005"
  Group = -> [Sketch167,Pad039,Sketch168,Groove018,Chamfer030]
  Origin = -> Origin025
  Placement = pos=(-138.956,-150.5,84.9639) rot=(0.862856,-0.357407,0.357407;1.71777rad)
  Tip = -> Chamfer030
FEATURE [PartDesign::Body] Body012  label="M2 Nut012"
  Group = -> [Sketch321,Pad095,Sketch322,Groove013,Chamfer037]
  Origin = -> Origin016
  Placement = pos=(-132.366,-135.25,71.5732) rot=(0.862856,0.357407,-0.357407;1.71777rad)
  Tip = -> Chamfer037
FEATURE [PartDesign::Body] Body053  label="red wire002"
  Group = -> [Sketch306,Pad103]
  Origin = -> Origin090
  Placement = pos=(0,25.15,0) rot=(0,0,1;0rad)
  Tip = -> Pad103
FEATURE [PartDesign::Body] Body054  label="Wrist"
  Group = -> [Sketch116,Pad021,Sketch117,Pocket087,Fillet031,Sketch118,Pocket088,Pad022,Sketch119,Pocket089,Sketch120,Pocket090,Fillet032,Sketch121,Pocket091,Sketch122,Pocket092,Sketch315,Sketch123,Pocket139,Pocket093,Chamfer,Sketch124,Pocket094,Fillet050]
  Origin = -> Origin084
  Placement = pos=(-66.468,-10,83.4386) rot=(0.281085,0.678598,0.678598;3.68962rad)
  Tip = -> Fillet050
FEATURE [PartDesign::Body] Body055  label="Foot_Tip"
  Group = -> [Sketch125,Pad098,Sketch318,Groove,Sketch002,SubtractivePipe003,PolarPattern,Sketch003,Groove015,Sketch004,Pocket095,Sketch005,Pocket141,Sketch006,Pocket142,Sketch007,Pocket140,Sketch316,Pocket143,Sketch314,Pocket005]
  Origin = -> Origin083
  Placement = pos=(0.75,0,37.62) rot=(0,1,0;3.14159rad)
  Tip = -> Pocket005
FEATURE [App::Part] Part002  label="Lower Leg and foot"
  Group = -> [Body054,Body055]
  Origin = -> Origin019
FEATURE [PartDesign::Body] Body011  label="Wrist_Counterpart"
  Group = -> [Sketch142,Pad028,Sketch139,Pocket098,Sketch143,Pocket100,Sketch324,Pocket102,Sketch138,Pocket099,Sketch140,Pocket104,Fillet035,Sketch323,Pocket101,Sketch144,Pocket103,Fillet036,Fillet037,Sketch141,Pad027,Fillet038]
  Origin = -> Origin015
  Placement = pos=(-115.966,-155,33.9411) rot=(0.382683,0,0.92388;3.14159rad)
  Tip = -> Fillet038
FEATURE [PartDesign::Body] Body003  label="M3 Nut"
  Group = -> [Sketch126,Pad023,Sketch127,Groove019,Chamfer001]
  Origin = -> Origin003
  Placement = pos=(0.75,-5.5,34.25) rot=(1,0,0;1.5708rad)
  Tip = -> Chamfer001
FEATURE [PartDesign::Body] Body013  label="Shoulder_Joint_Ball_Bearing_Pin"
  Group = -> [Sketch147,Pad029,Chamfer027]
  Origin = -> Origin018
  Placement = pos=(-132.396,-132.926,71.5546) rot=(-1,0,0;1.5708rad)
  Tip = -> Chamfer027
FEATURE [PartDesign::Body] Body008  label="M3 Nut001"
  Group = -> [Sketch128,Pad024,Sketch129,Groove020,Chamfer002]
  Origin = -> Origin082
  Placement = pos=(0.75,5.5,34.25) rot=(1,0,0;1.5708rad)
  Tip = -> Chamfer002
FEATURE [App::Part] Part025  label="Nuts"
  Group = -> [Body003,Body008]
  Origin = -> Origin013
FEATURE [PartDesign::Body] Body010  label="M3x009"
  Group = -> [Sketch319,Pad026,Sketch317,Pad025,Sketch320,Pocket097,Chamfer039]
  Origin = -> Origin012
  Placement = pos=(0.72,13.88,34.3) rot=(1,0,0;1.5708rad)
  Tip = -> Chamfer039
FEATURE [App::Part] Part026  label="Screws002"
  Group = -> [Body009,Body010]
  Origin = -> Origin014
FEATURE [PartDesign::Body] Body017  label="M3 Nut004"
  Group = -> [Sketch165,Pad038,Sketch166,Groove017,Chamfer028]
  Origin = -> Origin024
  Placement = pos=(-146.027,-150.5,78.1297) rot=(0.862856,-0.357407,0.357407;1.71777rad)
  Tip = -> Chamfer028
FEATURE [PartDesign::Body] Body016  label="M3 Nut003"
  Group = -> [Sketch163,Pad037,Sketch164,Groove016,Chamfer036]
  Origin = -> Origin023
  Placement = pos=(-104.661,-150.5,50.9359) rot=(0.862856,-0.357407,0.357407;1.71777rad)
  Tip = -> Chamfer036
FEATURE [PartDesign::Body] Body015  label="M3 Nut002"
  Group = -> [Sketch161,Pad036,Sketch162,Groove014,Chamfer035]
  Origin = -> Origin022
  Placement = pos=(-111.697,-150.5,43.8385) rot=(0.862856,-0.357407,0.357407;1.71777rad)
  Tip = -> Chamfer035
FEATURE [App::Part] Part003  label="Lower Leg Counterpiece and Ball Bearing Pin"
  Group = -> [Body011,Body012,Body052,Body013,Body015,Body016,Body017,Body018]
  Origin = -> Origin020
  Placement = pos=(49.45,155,49.5) rot=(0,0,1;0rad)
FEATURE [PartDesign::Body] Body005  label="M3x20"
  Group = -> [Sketch182,Pad046,Sketch183,Pad047,Sketch184,Pocket109,Chamfer033]
  Origin = -> Origin008
  Placement = pos=(-149,-30,75) rot=(-1,0,0;1.5708rad)
  Tip = -> Chamfer033
FEATURE [PartDesign::Body] Body020  label="M3x010"
  Group = -> [Sketch185,Pad048,Sketch186,Pad049,Sketch187,Pocket110,Chamfer031]
  Origin = -> Origin027
  Placement = pos=(-156,-30,68) rot=(-1,0,0;1.5708rad)
  Tip = -> Chamfer031
FEATURE [PartDesign::Body] Body021  label="M3x011"
  Group = -> [Sketch188,Pad050,Sketch189,Pad051,Sketch190,Pocket111,Chamfer032]
  Origin = -> Origin028
  Placement = pos=(-121.75,-30,34) rot=(-1,0,0;1.5708rad)
  Tip = -> Chamfer032
FEATURE [PartDesign::Body] Body022  label="M3x012"
  Group = -> [Sketch191,Pad052,Sketch192,Pad053,Sketch193,Pocket144,Chamfer034]
  Origin = -> Origin029
  Placement = pos=(-114.75,-30,41) rot=(-1,0,0;1.5708rad)
  Tip = -> Chamfer034
FEATURE [App::Part] Part004  label="m3x20 screws"
  Group = -> [Body005,Body020,Body021,Body022]
  Origin = -> Origin030
  Placement = pos=(59.5,12.25,59.5) rot=(0,0,1;0rad)
FEATURE [PartDesign::Body] Body056  label="Gear002"
  Group = -> [Sketch313,Pad105,Sketch305,Pocket149,Chamfer041]
  Origin = -> Origin086
  Placement = pos=(0,0,38.25) rot=(0,0,1;0rad)
  Tip = -> Chamfer041
FEATURE [PartDesign::Body] Body057  label="brown wire002"
  Group = -> [Sketch307,Pad109]
  Origin = -> Origin088
  Placement = pos=(0,25.15,0) rot=(0,0,1;0rad)
  Tip = -> Pad109
FEATURE [PartDesign::Body] Body058  label="MG996R001"
  Group = -> [Sketch309,Pad099,Sketch299,Pad112,Sketch300,Pad101,Sketch303,Pad102,Sketch296,Pad104,Sketch295,Pad108,Sketch311,Pad107,Sketch312,Pocket148,Sketch297,Pocket145,Sketch308,Pad111,Sketch310,Pocket147,Fillet049,Sketch302,Pad113,Sketch301,Pad100,Sketch298,Pad106,Chamfer040,Fillet048,Sketch294,Pocket146]
  Origin = -> Origin089
  Tip = -> Pocket146
FEATURE [PartDesign::Body] Body059  label="orange wire002"
  Group = -> [Sketch304,Pad110]
  Origin = -> Origin087
  Placement = pos=(0,25.15,0) rot=(0,0,1;0rad)
  Tip = -> Pad110
FEATURE [App::Part] Part024  label="Servo001"
  Group = -> [Body058,Body056,Body053,Body059,Body057]
  Origin = -> Origin085
  Placement = pos=(-75.5841,15.8,113.841) rot=(-0.862856,0.357407,-0.357407;4.56541rad)
FEATURE [Sketcher::SketchObject] Sketch159
  MapMode = 5
  Placement = pos=(0,0,0) rot=(0.57735,0.57735,0.57735;2.0944rad)
  Support = -> [YZ_Plane091]
  sketch-geometry (4):
    g0: LineSegment StartX=35.5 StartY=12.9 StartZ=0 EndX=38.5 EndY=12.9 EndZ=0
    g1: LineSegment StartX=38.5 StartY=12.9 StartZ=0 EndX=38.5 EndY=7.1 EndZ=0
    g2: LineSegment StartX=38.5 StartY=7.1 StartZ=0 EndX=35.5 EndY=7.1 EndZ=0
    g3: LineSegment StartX=35.5 StartY=7.1 StartZ=0 EndX=35.5 EndY=12.9 EndZ=0
  constraints (12):
    c: Coincident(g0,g1)
    c: Coincident(g1,g2)
    c: Coincident(g2,g3)
    c: Coincident(g3,g0)
    c: Horizontal(g0)
    c: Horizontal(g2)
    c: Vertical(g1)
    c: Vertical(g3)
    c: DistanceY(g-1,g1) = 7.1
    c: DistanceY(g3,g3) = 5.8
    c: DistanceX(g0,g0) = 3
    c: DistanceX(g-1,g1) = 38.5
FEATURE [Sketcher::SketchObject] Sketch160
  MapMode = 5
  Placement = pos=(0,0,0) rot=(0.57735,0.57735,0.57735;2.0944rad)
  Support = -> [YZ_Plane091]
  sketch-geometry (4):
    g0: LineSegment StartX=35.5 StartY=17.1 StartZ=0 EndX=38.5 EndY=17.1 EndZ=0
    g1: LineSegment StartX=38.5 StartY=17.1 StartZ=0 EndX=38.5 EndY=22.9 EndZ=0
    g2: LineSegment StartX=38.5 StartY=22.9 StartZ=0 EndX=35.5 EndY=22.9 EndZ=0
    g3: LineSegment StartX=35.5 StartY=22.9 StartZ=0 EndX=35.5 EndY=17.1 EndZ=0
  constraints (12):
    c: Coincident(g0,g1)
    c: Coincident(g1,g2)
    c: Coincident(g2,g3)
    c: Coincident(g3,g0)
    c: Horizontal(g0)
    c: Horizontal(g2)
    c: Vertical(g1)
    c: Vertical(g3)
    c: DistanceX(g2,g2) = 3
    c: DistanceY(g1,g1) = 5.8
    c: DistanceX(g-1,g0) = 38.5
    c: DistanceY(g-1,g0) = 17.1
FEATURE [Sketcher::SketchObject] Sketch328
  MapMode = 5
  Placement = pos=(0,0,0) rot=(1,0,0;1.5708rad)
  Support = -> [XZ_Plane091]
  sketch-geometry (4):
    g0: LineSegment StartX=68.5 StartY=25 StartZ=0 EndX=125 EndY=25 EndZ=0
    g1: LineSegment StartX=125 StartY=25 StartZ=0 EndX=125 EndY=5 EndZ=0
    g2: LineSegment StartX=125 StartY=5 StartZ=0 EndX=68.5 EndY=5 EndZ=0
    g3: LineSegment StartX=68.5 StartY=5 StartZ=0 EndX=68.5 EndY=25 EndZ=0
  constraints (12):
    c: Coincident(g0,g1)
    c: Coincident(g1,g2)
    c: Coincident(g2,g3)
    c: Coincident(g3,g0)
    c: Horizontal(g0)
    c: Horizontal(g2)
    c: Vertical(g1)
    c: Vertical(g3)
    c: DistanceX(g0,g0) = 56.5
    c: DistanceY(g3,g3) = 20
    c: DistanceY(g-1,g2) = 5
    c: DistanceX(g-1,g0) = 68.5
FEATURE [Sketcher::SketchObject] Sketch331
  MapMode = 5
  Support = -> [XY_Plane091]
  sketch-geometry (12):
    g0: LineSegment StartX=0 StartY=0 StartZ=0 EndX=0 EndY=57 EndZ=0
    g1: LineSegment StartX=0 StartY=57 StartZ=0 EndX=40 EndY=57 EndZ=0
    g2: ArcOfCircle CenterX=40 CenterY=44.5 CenterZ=0 NormalX=0 NormalY=0 NormalZ=1 AngleXU=0 Radius=12.5 StartAngle=0.643501 EndAngle=1.5708
    g3: ArcOfCircle CenterX=60 CenterY=59.5 CenterZ=0 NormalX=0 NormalY=0 NormalZ=1 AngleXU=0 Radius=12.5 StartAngle=3.78509 EndAngle=4.71239
    g4: LineSegment StartX=60 StartY=47 StartZ=0 EndX=120 EndY=47 EndZ=0
    g5: ArcOfCircle CenterX=120 CenterY=37 CenterZ=0 NormalX=0 NormalY=0 NormalZ=1 AngleXU=0 Radius=10 StartAngle=2e-16 EndAngle=1.5708
    g6: LineSegment StartX=130 StartY=37 StartZ=0 EndX=130 EndY=15 EndZ=0
    g7: ArcOfCircle CenterX=125 CenterY=15 CenterZ=0 NormalX=0 NormalY=0 NormalZ=1 AngleXU=0 Radius=5 StartAngle=4.71239 EndAngle=6.28319
    g8: LineSegment StartX=125 StartY=10 StartZ=0 EndX=60 EndY=10 EndZ=0
    g9: LineSegment StartX=40 StartY=0 StartZ=0 EndX=0 EndY=0 EndZ=0
    g10: ArcOfCircle CenterX=40 CenterY=12.5 CenterZ=0 NormalX=0 NormalY=0 NormalZ=1 AngleXU=0 Radius=12.5 StartAngle=4.71239 EndAngle=5.63968
    g11: ArcOfCircle CenterX=60 CenterY=-2.5 CenterZ=0 NormalX=0 NormalY=0 NormalZ=1 AngleXU=0 Radius=12.5 StartAngle=1.5708 EndAngle=2.49809
  constraints (31):
    c: Coincident(g-1,g0)
    c: PointOnObject(g0,g-2)
    c: Coincident(g0,g1)
    c: Horizontal(g1)
    c: Tangent(g1,g2) = 1.5708
    c: Tangent(g2,g3) = 1.5708
    c: Tangent(g3,g4) = -1.5708
    c: Tangent(g4,g5) = 1.5708
    c: Tangent(g5,g6) = 1.5708
    c: Tangent(g6,g7) = 1.5708
    c: Tangent(g7,g8) = 1.5708
    c: Coincident(g9,g0)
    c: Horizontal(g9)
    c: Horizontal(g4)
    c: Horizontal(g8)
    c: Vertical(g6)
    c: Tangent(g11,g8) = -1.5708
    c: Tangent(g11,g10) = 1.5708
    c: Radius(g7) = 5
    c: Radius(g5) = 10
    c: DistanceX(g1,g1) = 40
    c: DistanceX(g0,g6) = 130
    c: DistanceX(g1,g3) = 20
    c: Tangent(g10,g9) = 1.5708
    c: DistanceX(g9,g8) = 20
    c: DistanceX(g9,g9) = 40
    c: DistanceY(g0,g0) = 57
    c: DistanceY(g9,g8) = 10
    c: DistanceY(g3,g1) = 10
    c: DistanceX(g10,g8) = 10
    c: DistanceX(g2,g3) = 10
FEATURE [PartDesign::Pad] Pad115  label="Baseplate005"
  Length = 30
  Length2 = 100
  Profile = -> Sketch331
  Type = 0
FEATURE [PartDesign::Pocket] Pocket150  label="Servohorn Mount Pocket"
  BaseFeature = -> Pad115
  Length = 5
  Length2 = 100
  Profile = -> Pad115 [Face12]
  Type = 0
FEATURE [PartDesign::Pocket] Pocket151  label="Ball Bearing Mount Pocket"
  BaseFeature = -> Pocket150
  Length = 5
  Length2 = 100
  Profile = -> Pocket150 [Face3]
  Type = 0
FEATURE [Sketcher::SketchObject] Sketch329
  MapMode = 5
  Placement = pos=(40,0,0) rot=(0.57735,-0.57735,-0.57735;2.0944rad)
  Support = -> [Pocket151]
  sketch-geometry (6):
    g0: ArcOfCircle CenterX=-25.9999 CenterY=20 CenterZ=0 NormalX=0 NormalY=0 NormalZ=1 AngleXU=0 Radius=25.9999 StartAngle=6.28318 EndAngle=6.67798
    g1: LineSegment StartX=-2 StartY=30 StartZ=0 EndX=1 EndY=30 EndZ=0
    g2: LineSegment StartX=1 StartY=30 StartZ=0 EndX=1 EndY=0 EndZ=0
    g3: LineSegment StartX=1 StartY=0 StartZ=0 EndX=-2 EndY=2.39524e-11 EndZ=0
    g4: ArcOfCircle CenterX=-25.9999 CenterY=9.99999 CenterZ=0 NormalX=0 NormalY=0 NormalZ=1 AngleXU=0 Radius=25.9999 StartAngle=5.88839 EndAngle=6.28319
    g5: LineSegment StartX=-2.5011e-12 StartY=10 StartZ=0 EndX=-2.5011e-12 EndY=20 EndZ=0
  constraints (20):
    c: DistanceY(g0,g0) = 10
    c: DistanceX(g0,g-1) = 2
    c: Vertical(g0,g-1)
    c: Tangent(g0,g-2)
    c: DistanceY(g-1,g0) = 30
    c: Coincident(g0,g1)
    c: Coincident(g1,g2)
    c: PointOnObject(g2,g-1)
    c: Vertical(g2)
    c: Coincident(g2,g3)
    c: PointOnObject(g3,g-1)
    c: Coincident(g4,g3)
    c: Tangent(g4,g-2)
    c: Vertical(g3,g0)
    c: DistanceY(g-1,g4) = 10
    c: Coincident(g5,g4)
    c: Coincident(g5,g0)
    c: Vertical(g5)
    c: Horizontal(g1)
    c: DistanceX(g1,g1) = 3
FEATURE [PartDesign::SubtractivePipe] SubtractivePipe004  label="Smooth Beveled Surfaces"
  AuxilleryCurvelinear = true
  AuxillerySpineTangent = false
  BaseFeature = -> Pocket151
  Binormal = (0,0,0)
  Mode = 0
  Profile = -> Sketch329
  Spine = -> Pocket151 [Edge21,Edge22,Edge23,Edge24,Edge25,Edge26,Edge27,Edge28,Edge29]
  SpineTangent = false
  Transformation = 0
  Transition = 0
FEATURE [PartDesign::Fillet] Fillet052  label="Smooth Edges004"
  Base = -> SubtractivePipe004 [Edge20,Edge5]
  BaseFeature = -> SubtractivePipe004
  Radius = 1.5
FEATURE [Sketcher::SketchObject] Sketch327
  MapMode = 5
  Placement = pos=(0,5,0) rot=(1,0,0;1.5708rad)
  Support = -> [Fillet052]
  sketch-geometry (1):
    g0: Circle CenterX=0 CenterY=0 CenterZ=0 NormalX=0 NormalY=0 NormalZ=1 AngleXU=0 Radius=30
  constraints (2):
    c: Coincident(g0,g-1)
    c: Radius(g0) = 30
FEATURE [PartDesign::Pocket] Pocket039  label="Joint Pan"
  BaseFeature = -> Fillet052
  Length = 47
  Length2 = 100
  Profile = -> Sketch327
  Type = 0
FEATURE [Sketcher::SketchObject] Sketch326
  ExternalGeometry = -> [Pocket039]
  MapMode = 5
  Placement = pos=(0,5,0) rot=(1,0,0;1.5708rad)
  Support = -> [Pocket039]
  sketch-geometry (7):
    g0: ArcOfCircle CenterX=23.5 CenterY=28.2018 CenterZ=0 NormalX=0 NormalY=0 NormalZ=1 AngleXU=0 Radius=1.79818 StartAngle=1.57079 EndAngle=2.66896
    g1: LineSegment StartX=21.8989 StartY=29.0204 StartZ=0 EndX=19.5977 EndY=24.5195 EndZ=0
    g2: ArcOfCircle CenterX=21.1988 CenterY=23.701 CenterZ=0 NormalX=0 NormalY=0 NormalZ=1 AngleXU=0 Radius=1.79818 StartAngle=2.66896 EndAngle=3.98266
    g3: Circle [constr] CenterX=0 CenterY=0 CenterZ=0 NormalX=0 NormalY=0 NormalZ=1 AngleXU=0 Radius=30
    g4: LineSegment StartX=23.5 StartY=30 StartZ=0 EndX=0 EndY=30 EndZ=0
    g5: LineSegment StartX=0 StartY=30 StartZ=0 EndX=0 EndY=22.3607 EndZ=0
    g6: LineSegment StartX=0 StartY=22.3607 StartZ=0 EndX=20 EndY=22.3607 EndZ=0
  constraints (19):
    c: Coincident(g3,g-1)
    c: Radius(g3) = 30
    c: Coincident(g4,g0)
    c: PointOnObject(g4,g3)
    c: Horizontal(g4)
    c: Tangent(g4,g0)
    c: Coincident(g5,g4)
    c: Vertical(g5)
    c: Tangent(g2,g3) = 1.5708
    c: Tangent(g2,g1) = -1.5708
    c: Tangent(g1,g0) = -1.5708
    c: DistanceX(g4,g4) = 23.5
    c: PointOnObject(g4,g-2)
    c: DistanceX(g5,g2) = 20
    c: Equal(g0,g2)
    c: Coincident(g6,g5)
    c: Coincident(g6,g2)
    c: Horizontal(g6)
    c: Horizontal(g-3,g0)
FEATURE [PartDesign::Pocket] Pocket041  label="Shortened Angled Top"
  BaseFeature = -> Pocket039
  Length = 47
  Length2 = 100
  Profile = -> Sketch326
  Type = 0
FEATURE [PartDesign::Pocket] Pocket042  label="Servoplacement Helper Pocket"
  BaseFeature = -> Pocket041
  Length = 15
  Length2 = 100
  Profile = -> Sketch328
  Type = 0
FEATURE [PartDesign::Pad] Pad114  label="Servoplacement Helper Pad"
  BaseFeature = -> Pocket042
  Length = 5
  Length2 = 100
  Profile = -> Pocket042 [Face60]
  Type = 0
FEATURE [PartDesign::Fillet] Fillet053  label="Servoplacement Smooth Edges"
  Base = -> Pad114 [Edge121,Edge125]
  BaseFeature = -> Pad114
  Radius = 0.4
FEATURE [Sketcher::SketchObject] Sketch330
  MapMode = 5
  Placement = pos=(0,10,-2.2e-15) rot=(1,0,0;1.5708rad)
  Support = -> [Fillet053]
  sketch-geometry (4):
    g0: LineSegment StartX=76.5 StartY=25 StartZ=0 EndX=117 EndY=25 EndZ=0
    g1: LineSegment StartX=117 StartY=25 StartZ=0 EndX=117 EndY=5 EndZ=0
    g2: LineSegment StartX=117 StartY=5 StartZ=0 EndX=76.5 EndY=5 EndZ=0
    g3: LineSegment StartX=76.5 StartY=5 StartZ=0 EndX=76.5 EndY=25 EndZ=0
  constraints (12):
    c: Coincident(g0,g1)
    c: Coincident(g1,g2)
    c: Coincident(g2,g3)
    c: Coincident(g3,g0)
    c: Horizontal(g0)
    c: Horizontal(g2)
    c: Vertical(g1)
    c: Vertical(g3)
    c: DistanceX(g0,g0) = 40.5
    c: DistanceY(g3,g3) = 20
    c: DistanceY(g-1,g2) = 5
    c: DistanceX(g-1,g2) = 76.5
FEATURE [PartDesign::Pocket] Pocket043  label="Servo Pocket"
  BaseFeature = -> Fillet053
  Length = 30
  Length2 = 100
  Profile = -> Sketch330
  Type = 0
FEATURE [PartDesign::Fillet] Fillet051  label="Smooth Mount Edges"
  Base = -> Pocket043 [Edge147,Edge146,Edge141,Edge152]
  BaseFeature = -> Pocket043
  Radius = 0.4
FEATURE [Sketcher::SketchObject] Sketch150
  MapMode = 5
  Placement = pos=(0,0,30) rot=(0,0,1;0rad)
  Support = -> [Fillet051]
  sketch-geometry (4):
    g0: LineSegment StartX=0 StartY=0 StartZ=0 EndX=130 EndY=0 EndZ=0
    g1: LineSegment StartX=130 StartY=0 StartZ=0 EndX=130 EndY=57 EndZ=0
    g2: LineSegment StartX=130 StartY=57 StartZ=0 EndX=0 EndY=57 EndZ=0
    g3: LineSegment StartX=0 StartY=57 StartZ=0 EndX=0 EndY=0 EndZ=0
  constraints (11):
    c: Coincident(g0,g1)
    c: Coincident(g1,g2)
    c: Coincident(g2,g3)
    c: Coincident(g3,g0)
    c: Horizontal(g0)
    c: Horizontal(g2)
    c: Vertical(g1)
    c: Vertical(g3)
    c: Coincident(g0,g-1)
    c: DistanceY(g1,g1) = 57
    c: DistanceX(g2,g2) = 130
FEATURE [PartDesign::Pocket] Pocket050  label="Remove Top Surface"
  BaseFeature = -> Fillet051
  Length = 5
  Length2 = 100
  Profile = -> Sketch150
  Type = 0
FEATURE [Sketcher::SketchObject] Sketch151
  MapMode = 5
  Placement = pos=(0,0,25) rot=(0,0,1;0rad)
  Support = -> [Pocket050]
  sketch-geometry (7):
    g0: LineSegment StartX=0 StartY=43 StartZ=0 EndX=120 EndY=43 EndZ=0
    g1: ArcOfCircle CenterX=120 CenterY=38 CenterZ=0 NormalX=0 NormalY=0 NormalZ=1 AngleXU=0 Radius=5 StartAngle=3e-16 EndAngle=1.5708
    g2: LineSegment StartX=125 StartY=38 StartZ=0 EndX=125 EndY=10 EndZ=0
    g3: LineSegment StartX=125 StartY=10 StartZ=0 EndX=130 EndY=10 EndZ=0
    g4: LineSegment StartX=130 StartY=10 StartZ=0 EndX=130 EndY=57 EndZ=0
    g5: LineSegment StartX=130 StartY=57 StartZ=0 EndX=0 EndY=57 EndZ=0
    g6: LineSegment StartX=0 StartY=57 StartZ=0 EndX=0 EndY=43 EndZ=0
  constraints (20):
    c: Horizontal(g0)
    c: Tangent(g0,g1) = 1.5708
    c: Tangent(g1,g2) = 1.5708
    c: Coincident(g2,g3)
    c: Horizontal(g3)
    c: Coincident(g3,g4)
    c: Coincident(g4,g5)
    c: Horizontal(g5)
    c: Coincident(g5,g6)
    c: Coincident(g6,g0)
    c: Vertical(g6)
    c: Vertical(g4)
    c: Vertical(g2)
    c: PointOnObject(g0,g-2)
    c: DistanceY(g-1,g5) = 57
    c: DistanceX(g5,g5) = 130
    c: DistanceY(g-1,g3) = 10
    c: DistanceX(g3,g3) = 5
    c: Radius(g1) = 5
    c: DistanceY(g2,g0) = 33
FEATURE [PartDesign::Pocket] Pocket051  label="Remove Shell"
  BaseFeature = -> Pocket050
  Length = 25
  Length2 = 100
  Profile = -> Sketch151
  Type = 0
FEATURE [Sketcher::SketchObject] Sketch152
  MapMode = 5
  Placement = pos=(0,0,25) rot=(0,0,1;0rad)
  Support = -> [Pocket051]
  sketch-geometry (4):
    g0: LineSegment StartX=117 StartY=10 StartZ=0 EndX=125 EndY=10 EndZ=0
    g1: LineSegment StartX=125 StartY=10 StartZ=0 EndX=125 EndY=15 EndZ=0
    g2: LineSegment StartX=125 StartY=15 StartZ=0 EndX=117 EndY=15 EndZ=0
    g3: LineSegment StartX=117 StartY=15 StartZ=0 EndX=117 EndY=10 EndZ=0
  constraints (12):
    c: Coincident(g0,g1)
    c: Coincident(g1,g2)
    c: Coincident(g2,g3)
    c: Coincident(g3,g0)
    c: Horizontal(g0)
    c: Horizontal(g2)
    c: Vertical(g1)
    c: Vertical(g3)
    c: DistanceY(g1,g1) = 5
    c: DistanceX(g2,g2) = 8
    c: DistanceY(g-1,g0) = 10
    c: DistanceX(g-1,g2) = 117
FEATURE [PartDesign::Pocket] Pocket052  label="Remove Shell at Servopocket"
  BaseFeature = -> Pocket051
  Length = 20
  Length2 = 100
  Profile = -> Sketch152
  Type = 0
FEATURE [Sketcher::SketchObject] Sketch153
  MapMode = 5
  Placement = pos=(125,0,0) rot=(0.57735,0.57735,0.57735;2.0944rad)
  Support = -> [Pocket052]
  sketch-geometry (4):
    g0: LineSegment StartX=29.5 StartY=25 StartZ=0 EndX=34.5 EndY=25 EndZ=0
    g1: LineSegment StartX=29.5 StartY=25 StartZ=0 EndX=29.5 EndY=11.5 EndZ=0
    g2: LineSegment StartX=34.5 StartY=25 StartZ=0 EndX=34.5 EndY=11.5 EndZ=0
    g3: ArcOfCircle CenterX=32 CenterY=11.5 CenterZ=0 NormalX=0 NormalY=0 NormalZ=1 AngleXU=0 Radius=2.5 StartAngle=3.14159 EndAngle=6.28319
  constraints (11):
    c: Horizontal(g0)
    c: Coincident(g1,g0)
    c: Vertical(g1)
    c: Coincident(g2,g0)
    c: Vertical(g2)
    c: Tangent(g3,g1) = -1.5708
    c: Tangent(g3,g2) = 1.5708
    c: DistanceX(g0,g0) = 5
    c: DistanceY(g-1,g3) = 11.5
    c: DistanceX(g-1,g3) = 32
    c: DistanceY(g-1,g0) = 25
FEATURE [PartDesign::Pocket] Pocket053  label="Servocable"
  BaseFeature = -> Pocket052
  Length = 8
  Length2 = 100
  Profile = -> Sketch153
  Type = 0
FEATURE [Sketcher::SketchObject] Sketch154
  MapMode = 5
  Placement = pos=(125,0,0) rot=(0.57735,0.57735,0.57735;2.0944rad)
  Support = -> [Pocket053]
  sketch-geometry (8):
    g0: LineSegment StartX=18 StartY=22.9 StartZ=0 EndX=21 EndY=22.9 EndZ=0
    g1: LineSegment StartX=21 StartY=22.9 StartZ=0 EndX=21 EndY=17.1 EndZ=0
    g2: LineSegment StartX=21 StartY=17.1 StartZ=0 EndX=18 EndY=17.1 EndZ=0
    g3: LineSegment StartX=18 StartY=17.1 StartZ=0 EndX=18 EndY=22.9 EndZ=0
    g4: LineSegment StartX=18 StartY=12.9 StartZ=0 EndX=21 EndY=12.9 EndZ=0
    g5: LineSegment StartX=21 StartY=12.9 StartZ=0 EndX=21 EndY=7.1 EndZ=0
    g6: LineSegment StartX=21 StartY=7.1 StartZ=0 EndX=18 EndY=7.1 EndZ=0
    g7: LineSegment StartX=18 StartY=7.1 StartZ=0 EndX=18 EndY=12.9 EndZ=0
  constraints (24):
    c: Coincident(g0,g1)
    c: Coincident(g1,g2)
    c: Coincident(g2,g3)
    c: Coincident(g3,g0)
    c: Horizontal(g0)
    c: Horizontal(g2)
    c: Vertical(g1)
    c: Vertical(g3)
    c: Coincident(g4,g5)
    c: Coincident(g5,g6)
    c: Coincident(g6,g7)
    c: Coincident(g7,g4)
    c: Horizontal(g4)
    c: Horizontal(g6)
    c: Vertical(g5)
    c: Vertical(g7)
    c: Equal(g0,g4)
    c: Equal(g1,g5)
    c: Vertical(g4,g2)
    c: DistanceX(g-1,g6) = 18
    c: DistanceX(g6,g6) = 3
    c: DistanceY(g5,g5) = 5.8
    c: DistanceY(g4,g1) = 4.2
    c: DistanceY(g-1,g6) = 7.1
FEATURE [PartDesign::Pocket] Pocket054  label="Nutholes Servopocket"
  BaseFeature = -> Pocket053
  Length = 56.5
  Length2 = 100
  Profile = -> Sketch154
  Type = 0
FEATURE [Sketcher::SketchObject] Sketch155
  MapMode = 5
  Placement = pos=(0,10,-2.2e-15) rot=(1,0,0;1.5708rad)
  Support = -> [Pocket054]
  sketch-geometry (4):
    g0: Circle CenterX=72.5 CenterY=20 CenterZ=0 NormalX=0 NormalY=0 NormalZ=1 AngleXU=0 Radius=1.6
    g1: Circle CenterX=72.5 CenterY=10 CenterZ=0 NormalX=0 NormalY=0 NormalZ=1 AngleXU=0 Radius=1.6
    g2: Circle CenterX=121 CenterY=20 CenterZ=0 NormalX=0 NormalY=0 NormalZ=1 AngleXU=0 Radius=1.6
    g3: Circle CenterX=121 CenterY=10 CenterZ=0 NormalX=0 NormalY=0 NormalZ=1 AngleXU=0 Radius=1.6
  constraints (12):
    c: Vertical(g3,g2)
    c: Vertical(g1,g0)
    c: Horizontal(g0,g2)
    c: Horizontal(g1,g3)
    c: Equal(g0,g1)
    c: Equal(g1,g2)
    c: Equal(g2,g3)
    c: Radius(g2) = 1.6
    c: DistanceY(g1,g0) = 10
    c: DistanceY(g-1,g1) = 10
    c: DistanceX(g1,g3) = 48.5
    c: DistanceX(g-1,g1) = 72.5
FEATURE [PartDesign::Pocket] Pocket055  label="Screwholes Servopocket"
  BaseFeature = -> Pocket054
  Length = 18
  Length2 = 100
  Profile = -> Sketch155
  Type = 0
FEATURE [Sketcher::SketchObject] Sketch156
  MapMode = 5
  Placement = pos=(0,5,0) rot=(1,0,0;1.5708rad)
  Support = -> [Pocket055]
  sketch-geometry (3):
    g0: Circle [constr] CenterX=0 CenterY=0 CenterZ=0 NormalX=0 NormalY=0 NormalZ=1 AngleXU=0 Radius=35
    g1: Circle CenterX=33.541 CenterY=10 CenterZ=0 NormalX=0 NormalY=0 NormalZ=1 AngleXU=0 Radius=1.6
    g2: Circle CenterX=28.7228 CenterY=20 CenterZ=0 NormalX=0 NormalY=0 NormalZ=1 AngleXU=0 Radius=1.6
  constraints (8):
    c: Coincident(g0,g-1)
    c: Radius(g0) = 35
    c: PointOnObject(g1,g0)
    c: PointOnObject(g2,g0)
    c: Equal(g2,g1)
    c: Radius(g2) = 1.6
    c: DistanceY(g1,g2) = 10
    c: DistanceY(g-1,g1) = 10
FEATURE [PartDesign::Pocket] Pocket056  label="Screwholes Servohorn Mount"
  BaseFeature = -> Pocket055
  Length = 20
  Length2 = 100
  Profile = -> Sketch156
  Type = 0
FEATURE [Sketcher::SketchObject] Sketch157
  MapMode = 5
  Placement = pos=(0,43,0) rot=(0,0.707107,0.707107;3.14159rad)
  Support = -> [Pocket056]
  sketch-geometry (3):
    g0: Circle [constr] CenterX=0 CenterY=0 CenterZ=0 NormalX=0 NormalY=0 NormalZ=1 AngleXU=0 Radius=35
    g1: Circle CenterX=-33.541 CenterY=10 CenterZ=0 NormalX=0 NormalY=0 NormalZ=1 AngleXU=0 Radius=1.6
    g2: Circle CenterX=-28.7228 CenterY=20 CenterZ=0 NormalX=0 NormalY=0 NormalZ=1 AngleXU=0 Radius=1.6
  constraints (8):
    c: Coincident(g0,g-1)
    c: Radius(g0) = 35
    c: PointOnObject(g1,g0)
    c: PointOnObject(g2,g0)
    c: Equal(g2,g1)
    c: Radius(g2) = 1.6
    c: DistanceY(g1,g2) = 10
    c: DistanceY(g-1,g1) = 10
FEATURE [PartDesign::Pocket] Pocket057  label="Screwholes Ball Bearing Mount"
  BaseFeature = -> Pocket056
  Length = 10
  Length2 = 100
  Profile = -> Sketch157
  Type = 0
FEATURE [Sketcher::SketchObject] Sketch158
  MapMode = 5
  Placement = pos=(0,0,25) rot=(0,0,1;0rad)
  Support = -> [Pocket057]
  sketch-geometry (6):
    g0: LineSegment StartX=0 StartY=14 StartZ=0 EndX=40 EndY=14 EndZ=0
    g1: LineSegment StartX=40 StartY=14 StartZ=0 EndX=40 EndY=26 EndZ=0
    g2: LineSegment StartX=0 StartY=31 StartZ=0 EndX=0 EndY=14 EndZ=0
    g3: LineSegment StartX=40 StartY=26 StartZ=0 EndX=67.5 EndY=26 EndZ=0
    g4: LineSegment StartX=67.5 StartY=26 StartZ=0 EndX=67.5 EndY=31 EndZ=0
    g5: LineSegment StartX=67.5 StartY=31 StartZ=0 EndX=0 EndY=31 EndZ=0
  constraints (18):
    c: Coincident(g0,g1)
    c: Coincident(g2,g0)
    c: Horizontal(g0)
    c: Vertical(g1)
    c: Vertical(g2)
    c: PointOnObject(g0,g-2)
    c: DistanceY(g1,g2) = 17
    c: DistanceY(g-1,g0) = 14
    c: Horizontal(g3)
    c: Coincident(g4,g3)
    c: Vertical(g4)
    c: Horizontal(g5)
    c: Coincident(g4,g5)
    c: Coincident(g1,g3)
    c: Coincident(g5,g2)
    c: DistanceX(g-1,g4) = 67.5
    c: DistanceY(g4,g4) = 5
    c: DistanceX(g0,g0) = 40
FEATURE [PartDesign::Pocket] Pocket058  label="Interlock"
  BaseFeature = -> Pocket057
  Length = 20
  Length2 = 100
  Profile = -> Sketch158
  Type = 0
FEATURE [PartDesign::Pocket] Pocket059  label="Bottom Nuthole Ball Bearing Mount"
  BaseFeature = -> Pocket058
  Length = 38
  Length2 = 100
  Profile = -> Sketch159
  Reversed = true
  Type = 0
FEATURE [PartDesign::Pocket] Pocket060  label="Top Nuthole Ball Bearing Mount"
  BaseFeature = -> Pocket059
  Length = 33
  Length2 = 100
  Profile = -> Sketch160
  Reversed = true
  Type = 0
FEATURE [PartDesign::Fillet] Fillet009  label="Smooth Interlock"
  Base = -> Pocket060 [Edge21,Edge15,Edge85,Edge118,Edge117,Edge116,Edge75,Edge13,Edge76,Edge178,Edge179,Edge88,Edge84,Edge83,Edge82,Edge81,Edge14,Edge72,Edge78,Edge87,Edge86]
  BaseFeature = -> Pocket060
  Radius = 0.4
FEATURE [PartDesign::Fillet] Fillet010  label="Smooth Servopocket"
  Base = -> Fillet009 [Edge244,Edge256,Edge257,Edge246,Edge255]
  BaseFeature = -> Fillet009
  Radius = 1
FEATURE [PartDesign::Fillet] Fillet011  label="Smooth Servocable Edges"
  Base = -> Fillet010 [Edge10,Edge199]
  BaseFeature = -> Fillet010
  Radius = 2.5
FEATURE [PartDesign::Body] Body060  label="Limb_Bottom_Shell"
  Group = -> [Sketch331,Pad115,Pocket150,Pocket151,Sketch329,SubtractivePipe004,Fillet052,Sketch327,Pocket039,Sketch326,Pocket041,Sketch328,Pocket042,Pad114,Fillet053,Sketch330,Pocket043,Fillet051,Sketch150,Pocket050,Sketch151,Pocket051,Sketch152,Pocket052,Sketch153,Pocket053,Sketch154,Pocket054,Sketch155,Pocket055,Sketch156,Pocket056,Sketch157,Pocket057,Sketch158,Pocket058,Sketch159,Pocket059,Sketch160,+4 more]
  Origin = -> Origin091
  Placement = pos=(-144.05,-29.45,42.05) rot=(0,0,1;0rad)
  Tip = -> Fillet011
FEATURE [Sketcher::SketchObject] Sketch333
  MapMode = 5
  Support = -> [XY_Plane092]
  sketch-geometry (12):
    g0: LineSegment StartX=0 StartY=0 StartZ=0 EndX=0 EndY=57 EndZ=0
    g1: LineSegment StartX=0 StartY=57 StartZ=0 EndX=40 EndY=57 EndZ=0
    g2: ArcOfCircle CenterX=40 CenterY=44.5 CenterZ=0 NormalX=0 NormalY=0 NormalZ=1 AngleXU=0 Radius=12.5 StartAngle=0.643501 EndAngle=1.5708
    g3: ArcOfCircle CenterX=60 CenterY=59.5 CenterZ=0 NormalX=0 NormalY=0 NormalZ=1 AngleXU=0 Radius=12.5 StartAngle=3.78509 EndAngle=4.71239
    g4: LineSegment StartX=60 StartY=47 StartZ=0 EndX=120 EndY=47 EndZ=0
    g5: ArcOfCircle CenterX=120 CenterY=37 CenterZ=0 NormalX=0 NormalY=0 NormalZ=1 AngleXU=0 Radius=10 StartAngle=2e-16 EndAngle=1.5708
    g6: LineSegment StartX=130 StartY=37 StartZ=0 EndX=130 EndY=15 EndZ=0
    g7: ArcOfCircle CenterX=125 CenterY=15 CenterZ=0 NormalX=0 NormalY=0 NormalZ=1 AngleXU=0 Radius=5 StartAngle=4.71239 EndAngle=6.28319
    g8: LineSegment StartX=125 StartY=10 StartZ=0 EndX=60 EndY=10 EndZ=0
    g9: LineSegment StartX=40 StartY=0 StartZ=0 EndX=0 EndY=0 EndZ=0
    g10: ArcOfCircle CenterX=40 CenterY=12.5 CenterZ=0 NormalX=0 NormalY=0 NormalZ=1 AngleXU=0 Radius=12.5 StartAngle=4.71239 EndAngle=5.63968
    g11: ArcOfCircle CenterX=60 CenterY=-2.5 CenterZ=0 NormalX=0 NormalY=0 NormalZ=1 AngleXU=0 Radius=12.5 StartAngle=1.5708 EndAngle=2.49809
  constraints (31):
    c: Coincident(g-1,g0)
    c: PointOnObject(g0,g-2)
    c: Coincident(g0,g1)
    c: Horizontal(g1)
    c: Tangent(g1,g2) = 1.5708
    c: Tangent(g2,g3) = 1.5708
    c: Tangent(g3,g4) = -1.5708
    c: Tangent(g4,g5) = 1.5708
    c: Tangent(g5,g6) = 1.5708
    c: Tangent(g6,g7) = 1.5708
    c: Tangent(g7,g8) = 1.5708
    c: Coincident(g9,g0)
    c: Horizontal(g9)
    c: Horizontal(g4)
    c: Horizontal(g8)
    c: Vertical(g6)
    c: Tangent(g11,g8) = -1.5708
    c: Tangent(g11,g10) = 1.5708
    c: Radius(g7) = 5
    c: Radius(g5) = 10
    c: DistanceX(g1,g1) = 40
    c: DistanceX(g0,g6) = 130
    c: DistanceX(g1,g3) = 20
    c: Tangent(g10,g9) = 1.5708
    c: DistanceX(g9,g8) = 20
    c: DistanceX(g9,g9) = 40
    c: DistanceY(g0,g0) = 57
    c: DistanceY(g9,g8) = 10
    c: DistanceY(g3,g1) = 10
    c: DistanceX(g10,g8) = 10
    c: DistanceX(g2,g3) = 10
FEATURE [Sketcher::SketchObject] Sketch337
  MapMode = 5
  Placement = pos=(0,0,0) rot=(1,0,0;1.5708rad)
  Support = -> [XZ_Plane092]
  sketch-geometry (4):
    g0: LineSegment StartX=68.5 StartY=25 StartZ=0 EndX=125 EndY=25 EndZ=0
    g1: LineSegment StartX=125 StartY=25 StartZ=0 EndX=125 EndY=5 EndZ=0
    g2: LineSegment StartX=125 StartY=5 StartZ=0 EndX=68.5 EndY=5 EndZ=0
    g3: LineSegment StartX=68.5 StartY=5 StartZ=0 EndX=68.5 EndY=25 EndZ=0
  constraints (12):
    c: Coincident(g0,g1)
    c: Coincident(g1,g2)
    c: Coincident(g2,g3)
    c: Coincident(g3,g0)
    c: Horizontal(g0)
    c: Horizontal(g2)
    c: Vertical(g1)
    c: Vertical(g3)
    c: DistanceX(g0,g0) = 56.5
    c: DistanceY(g3,g3) = 20
    c: DistanceY(g-1,g2) = 5
    c: DistanceX(g-1,g0) = 68.5
FEATURE [Sketcher::SketchObject] Sketch341
  MapMode = 5
  Placement = pos=(0,0,0) rot=(0.57735,0.57735,0.57735;2.0944rad)
  Support = -> [YZ_Plane092]
  sketch-geometry (4):
    g0: LineSegment StartX=18.5 StartY=7.1 StartZ=0 EndX=21.5 EndY=7.1 EndZ=0
    g1: LineSegment StartX=21.5 StartY=7.1 StartZ=0 EndX=21.5 EndY=12.9 EndZ=0
    g2: LineSegment StartX=21.5 StartY=12.9 StartZ=0 EndX=18.5 EndY=12.9 EndZ=0
    g3: LineSegment StartX=18.5 StartY=12.9 StartZ=0 EndX=18.5 EndY=7.1 EndZ=0
  constraints (12):
    c: Coincident(g0,g1)
    c: Coincident(g1,g2)
    c: Coincident(g2,g3)
    c: Coincident(g3,g0)
    c: Horizontal(g0)
    c: Horizontal(g2)
    c: Vertical(g1)
    c: Vertical(g3)
    c: DistanceX(g2,g2) = 3
    c: DistanceY(g1,g1) = 5.8
    c: DistanceY(g-1,g0) = 7.1
    c: DistanceX(g-1,g0) = 21.5
FEATURE [Sketcher::SketchObject] Sketch342
  MapMode = 5
  Placement = pos=(0,0,0) rot=(0.57735,0.57735,0.57735;2.0944rad)
  Support = -> [YZ_Plane092]
  sketch-geometry (4):
    g0: LineSegment StartX=18.5 StartY=17.1 StartZ=0 EndX=21.5 EndY=17.1 EndZ=0
    g1: LineSegment StartX=21.5 StartY=17.1 StartZ=0 EndX=21.5 EndY=22.9 EndZ=0
    g2: LineSegment StartX=21.5 StartY=22.9 StartZ=0 EndX=18.5 EndY=22.9 EndZ=0
    g3: LineSegment StartX=18.5 StartY=22.9 StartZ=0 EndX=18.5 EndY=17.1 EndZ=0
  constraints (12):
    c: Coincident(g0,g1)
    c: Coincident(g1,g2)
    c: Coincident(g2,g3)
    c: Coincident(g3,g0)
    c: Horizontal(g0)
    c: Horizontal(g2)
    c: Vertical(g1)
    c: Vertical(g3)
    c: DistanceX(g2,g2) = 3
    c: DistanceY(g1,g1) = 5.8
    c: DistanceX(g-1,g0) = 21.5
    c: DistanceY(g-1,g0) = 17.1
FEATURE [PartDesign::Pad] Pad117  label="Baseplate006"
  Length = 30
  Length2 = 100
  Profile = -> Sketch333
  Type = 0
FEATURE [PartDesign::Pocket] Pocket154  label="Servohorn Mount Pocket001"
  BaseFeature = -> Pad117
  Length = 5
  Length2 = 100
  Profile = -> Pad117 [Face12]
  Type = 0
FEATURE [PartDesign::Pocket] Pocket153  label="Ball Bearing Mount Pocket001"
  BaseFeature = -> Pocket154
  Length = 5
  Length2 = 100
  Profile = -> Pocket154 [Face3]
  Type = 0
FEATURE [Sketcher::SketchObject] Sketch334
  MapMode = 5
  Placement = pos=(40,0,0) rot=(0.57735,-0.57735,-0.57735;2.0944rad)
  Support = -> [Pocket153]
  sketch-geometry (6):
    g0: ArcOfCircle CenterX=-25.9999 CenterY=20 CenterZ=0 NormalX=0 NormalY=0 NormalZ=1 AngleXU=0 Radius=25.9999 StartAngle=6.28318 EndAngle=6.67798
    g1: LineSegment StartX=-2 StartY=30 StartZ=0 EndX=1 EndY=30 EndZ=0
    g2: LineSegment StartX=1 StartY=30 StartZ=0 EndX=1 EndY=0 EndZ=0
    g3: LineSegment StartX=1 StartY=0 StartZ=0 EndX=-2 EndY=2.39524e-11 EndZ=0
    g4: ArcOfCircle CenterX=-25.9999 CenterY=9.99999 CenterZ=0 NormalX=0 NormalY=0 NormalZ=1 AngleXU=0 Radius=25.9999 StartAngle=5.88839 EndAngle=6.28319
    g5: LineSegment StartX=-2.5011e-12 StartY=10 StartZ=0 EndX=-2.5011e-12 EndY=20 EndZ=0
  constraints (20):
    c: DistanceY(g0,g0) = 10
    c: DistanceX(g0,g-1) = 2
    c: Vertical(g0,g-1)
    c: Tangent(g0,g-2)
    c: DistanceY(g-1,g0) = 30
    c: Coincident(g0,g1)
    c: Coincident(g1,g2)
    c: PointOnObject(g2,g-1)
    c: Vertical(g2)
    c: Coincident(g2,g3)
    c: PointOnObject(g3,g-1)
    c: Coincident(g4,g3)
    c: Tangent(g4,g-2)
    c: Vertical(g3,g0)
    c: DistanceY(g-1,g4) = 10
    c: Coincident(g5,g4)
    c: Coincident(g5,g0)
    c: Vertical(g5)
    c: Horizontal(g1)
    c: DistanceX(g1,g1) = 3
FEATURE [PartDesign::SubtractivePipe] SubtractivePipe005  label="Smooth Beveled Surfaces001"
  AuxilleryCurvelinear = true
  AuxillerySpineTangent = false
  BaseFeature = -> Pocket153
  Binormal = (0,0,0)
  Mode = 0
  Profile = -> Sketch334
  Spine = -> Pocket153 [Edge21,Edge22,Edge23,Edge24,Edge25,Edge26,Edge27,Edge28,Edge29]
  SpineTangent = false
  Transformation = 0
  Transition = 0
FEATURE [PartDesign::Fillet] Fillet058  label="Smooth Edges005"
  Base = -> SubtractivePipe005 [Edge20,Edge5]
  BaseFeature = -> SubtractivePipe005
  Radius = 1.5
FEATURE [Sketcher::SketchObject] Sketch332
  MapMode = 5
  Placement = pos=(0,5,0) rot=(1,0,0;1.5708rad)
  Support = -> [Fillet058]
  sketch-geometry (1):
    g0: Circle CenterX=0 CenterY=0 CenterZ=0 NormalX=0 NormalY=0 NormalZ=1 AngleXU=0 Radius=30
  constraints (2):
    c: Coincident(g0,g-1)
    c: Radius(g0) = 30
FEATURE [PartDesign::Pocket] Pocket152  label="Joint Pan001"
  BaseFeature = -> Fillet058
  Length = 47
  Length2 = 100
  Profile = -> Sketch332
  Type = 0
FEATURE [Sketcher::SketchObject] Sketch335
  ExternalGeometry = -> [Pocket152]
  MapMode = 5
  Placement = pos=(0,5,0) rot=(1,0,0;1.5708rad)
  Support = -> [Pocket152]
  sketch-geometry (7):
    g0: ArcOfCircle CenterX=23.5 CenterY=28.2018 CenterZ=0 NormalX=0 NormalY=0 NormalZ=1 AngleXU=0 Radius=1.79818 StartAngle=1.57079 EndAngle=2.66896
    g1: LineSegment StartX=21.8989 StartY=29.0204 StartZ=0 EndX=19.5977 EndY=24.5195 EndZ=0
    g2: ArcOfCircle CenterX=21.1988 CenterY=23.701 CenterZ=0 NormalX=0 NormalY=0 NormalZ=1 AngleXU=0 Radius=1.79818 StartAngle=2.66896 EndAngle=3.98266
    g3: Circle [constr] CenterX=0 CenterY=0 CenterZ=0 NormalX=0 NormalY=0 NormalZ=1 AngleXU=0 Radius=30
    g4: LineSegment StartX=23.5 StartY=30 StartZ=0 EndX=0 EndY=30 EndZ=0
    g5: LineSegment StartX=0 StartY=30 StartZ=0 EndX=0 EndY=22.3607 EndZ=0
    g6: LineSegment StartX=0 StartY=22.3607 StartZ=0 EndX=20 EndY=22.3607 EndZ=0
  constraints (19):
    c: Coincident(g3,g-1)
    c: Radius(g3) = 30
    c: Coincident(g4,g0)
    c: PointOnObject(g4,g3)
    c: Horizontal(g4)
    c: Tangent(g4,g0)
    c: Coincident(g5,g4)
    c: Vertical(g5)
    c: Tangent(g2,g3) = 1.5708
    c: Tangent(g2,g1) = -1.5708
    c: Tangent(g1,g0) = -1.5708
    c: DistanceX(g4,g4) = 23.5
    c: PointOnObject(g4,g-2)
    c: DistanceX(g5,g2) = 20
    c: Equal(g0,g2)
    c: Coincident(g6,g5)
    c: Coincident(g6,g2)
    c: Horizontal(g6)
    c: Horizontal(g-3,g0)
FEATURE [PartDesign::Pocket] Pocket155  label="Shortened Angled Top001"
  BaseFeature = -> Pocket152
  Length = 47
  Length2 = 100
  Profile = -> Sketch335
  Type = 0
FEATURE [PartDesign::Pocket] Pocket156  label="Servoplacement Helper Pocket001"
  BaseFeature = -> Pocket155
  Length = 15
  Length2 = 100
  Profile = -> Sketch337
  Type = 0
FEATURE [PartDesign::Pad] Pad116  label="Servoplacement Helper Pad001"
  BaseFeature = -> Pocket156
  Length = 5
  Length2 = 100
  Profile = -> Pocket156 [Face60]
  Type = 0
FEATURE [PartDesign::Fillet] Fillet057  label="Servoplacement Smooth Edges001"
  Base = -> Pad116 [Edge121,Edge125]
  BaseFeature = -> Pad116
  Radius = 0.4
FEATURE [Sketcher::SketchObject] Sketch336
  MapMode = 5
  Placement = pos=(0,10,-2.2e-15) rot=(1,0,0;1.5708rad)
  Support = -> [Fillet057]
  sketch-geometry (4):
    g0: LineSegment StartX=76.5 StartY=25 StartZ=0 EndX=117 EndY=25 EndZ=0
    g1: LineSegment StartX=117 StartY=25 StartZ=0 EndX=117 EndY=5 EndZ=0
    g2: LineSegment StartX=117 StartY=5 StartZ=0 EndX=76.5 EndY=5 EndZ=0
    g3: LineSegment StartX=76.5 StartY=5 StartZ=0 EndX=76.5 EndY=25 EndZ=0
  constraints (12):
    c: Coincident(g0,g1)
    c: Coincident(g1,g2)
    c: Coincident(g2,g3)
    c: Coincident(g3,g0)
    c: Horizontal(g0)
    c: Horizontal(g2)
    c: Vertical(g1)
    c: Vertical(g3)
    c: DistanceX(g0,g0) = 40.5
    c: DistanceY(g3,g3) = 20
    c: DistanceY(g-1,g2) = 5
    c: DistanceX(g-1,g2) = 76.5
FEATURE [PartDesign::Pocket] Pocket167  label="Servo Pocket001"
  BaseFeature = -> Fillet057
  Length = 30
  Length2 = 100
  Profile = -> Sketch336
  Type = 0
FEATURE [PartDesign::Fillet] Fillet055  label="Smooth Mount Edges001"
  Base = -> Pocket167 [Edge147,Edge146,Edge141,Edge152]
  BaseFeature = -> Pocket167
  Radius = 0.4
FEATURE [Sketcher::SketchObject] Sketch339
  MapMode = 5
  Placement = pos=(0,0,0) rot=(1,0,0;3.14159rad)
  Support = -> [Fillet055]
  sketch-geometry (11):
    g0: LineSegment StartX=0 StartY=-43.25 StartZ=0 EndX=120.25 EndY=-43.25 EndZ=0
    g1: ArcOfCircle CenterX=120.25 CenterY=-38.25 CenterZ=0 NormalX=0 NormalY=0 NormalZ=1 AngleXU=0 Radius=5 StartAngle=4.71239 EndAngle=6.28319
    g2: LineSegment StartX=125.25 StartY=-38.25 StartZ=0 EndX=125.25 EndY=-14.75 EndZ=0
    g3: LineSegment StartX=125.25 StartY=-14.75 StartZ=0 EndX=117 EndY=-14.75 EndZ=0
    g4: LineSegment StartX=117 StartY=-14.75 StartZ=0 EndX=117 EndY=0 EndZ=0
    g5: LineSegment StartX=117 StartY=0 StartZ=0 EndX=0 EndY=0 EndZ=0
    g6: LineSegment StartX=0 StartY=0 StartZ=0 EndX=0 EndY=-14.25 EndZ=0
    g7: LineSegment StartX=0 StartY=-14.25 StartZ=0 EndX=39.75 EndY=-14.25 EndZ=0
    g8: LineSegment StartX=39.75 StartY=-14.25 StartZ=0 EndX=39.75 EndY=-25.75 EndZ=0
    g9: LineSegment StartX=39.75 StartY=-25.75 StartZ=0 EndX=0 EndY=-25.75 EndZ=0
    g10: LineSegment StartX=0 StartY=-25.75 StartZ=0 EndX=0 EndY=-43.25 EndZ=0
  constraints (30):
    c: PointOnObject(g0,g-2)
    c: Horizontal(g0)
    c: Tangent(g0,g1) = -1.5708
    c: Tangent(g1,g2) = -1.5708
    c: Coincident(g2,g3)
    c: Coincident(g3,g4)
    c: Coincident(g4,g5)
    c: Coincident(g5,g-1)
    c: Coincident(g5,g6)
    c: Coincident(g10,g0)
    c: Horizontal(g3)
    c: Vertical(g4)
    c: Vertical(g2)
    c: Horizontal(g5)
    c: DistanceX(g5,g2) = 125.25
    c: Radius(g1) = 5
    c: DistanceY(g4,g4) = 14.75
    c: DistanceX(g3,g3) = 8.25
    c: DistanceY(g0,g4) = 43.25
    c: Horizontal(g7)
    c: Coincident(g7,g8)
    c: Vertical(g8)
    c: Coincident(g8,g9)
    c: Horizontal(g9)
    c: Coincident(g6,g7)
    c: Tangent(g6,g10)
    c: DistanceY(g8,g8) = 11.5
    c: DistanceX(g7,g7) = 39.75
    c: DistanceY(g6,g5) = 14.25
    c: Coincident(g9,g10)
FEATURE [PartDesign::Pocket] Pocket166  label="Bottom Removal and Interlock"
  BaseFeature = -> Fillet055
  Length = 25
  Length2 = 100
  Profile = -> Sketch339
  Type = 0
FEATURE [Sketcher::SketchObject] Sketch338
  MapMode = 5
  Placement = pos=(0,0,0) rot=(1,0,0;3.14159rad)
  Support = -> [Pocket166]
  sketch-geometry (4):
    g0: LineSegment StartX=0 StartY=-26 StartZ=0 EndX=40 EndY=-26 EndZ=0
    g1: LineSegment StartX=40 StartY=-26 StartZ=0 EndX=40 EndY=-14 EndZ=0
    g2: LineSegment StartX=40 StartY=-14 StartZ=0 EndX=0 EndY=-14 EndZ=0
    g3: LineSegment StartX=0 StartY=-14 StartZ=0 EndX=0 EndY=-26 EndZ=0
  constraints (12):
    c: Coincident(g0,g1)
    c: Coincident(g1,g2)
    c: Coincident(g2,g3)
    c: Coincident(g3,g0)
    c: Horizontal(g0)
    c: Horizontal(g2)
    c: Vertical(g1)
    c: Vertical(g3)
    c: PointOnObject(g0,g-2)
    c: DistanceY(g1,g1) = 12
    c: DistanceY(g2,g-1) = 14
    c: DistanceX(g0,g0) = 40
FEATURE [PartDesign::Pocket] Pocket160  label="Shorten Interlock"
  BaseFeature = -> Pocket166
  Length = 5
  Length2 = 100
  Profile = -> Sketch338
  Type = 0
FEATURE [Sketcher::SketchObject] Sketch343
  MapMode = 5
  Placement = pos=(0,52,0) rot=(0,0.707107,0.707107;3.14159rad)
  Support = -> [Pocket160]
  sketch-geometry (3):
    g0: Circle [constr] CenterX=0 CenterY=0 CenterZ=0 NormalX=0 NormalY=0 NormalZ=1 AngleXU=0 Radius=35
    g1: Circle CenterX=-28.7228 CenterY=20 CenterZ=0 NormalX=0 NormalY=0 NormalZ=1 AngleXU=0 Radius=1.6
    g2: Circle CenterX=-33.541 CenterY=10 CenterZ=0 NormalX=0 NormalY=0 NormalZ=1 AngleXU=0 Radius=1.6
  constraints (8):
    c: Coincident(g0,g-1)
    c: Radius(g0) = 35
    c: PointOnObject(g1,g0)
    c: PointOnObject(g2,g0)
    c: Equal(g2,g1)
    c: Radius(g1) = 1.6
    c: DistanceY(g2,g1) = 10
    c: DistanceY(g-1,g2) = 10
FEATURE [PartDesign::Pocket] Pocket158  label="Screwholes Ball Bearing Mount (Interlock)"
  BaseFeature = -> Pocket160
  Length = 22
  Length2 = 100
  Profile = -> Sketch343
  Type = 0
FEATURE [Sketcher::SketchObject] Sketch340
  MapMode = 5
  Placement = pos=(0,14.25,0) rot=(1,0,0;1.5708rad)
  Support = -> [Pocket158]
  sketch-geometry (3):
    g0: Circle [constr] CenterX=0 CenterY=0 CenterZ=0 NormalX=0 NormalY=0 NormalZ=1 AngleXU=0 Radius=35
    g1: Circle CenterX=28.7228 CenterY=20 CenterZ=0 NormalX=0 NormalY=0 NormalZ=1 AngleXU=0 Radius=1.6
    g2: Circle CenterX=33.541 CenterY=10 CenterZ=0 NormalX=0 NormalY=0 NormalZ=1 AngleXU=0 Radius=1.6
  constraints (8):
    c: Coincident(g0,g-1)
    c: PointOnObject(g1,g0)
    c: PointOnObject(g2,g0)
    c: Equal(g2,g1)
    c: Radius(g1) = 1.6
    c: DistanceY(g2,g1) = 10
    c: DistanceY(g-1,g2) = 10
    c: Radius(g0) = 35
FEATURE [PartDesign::Pocket] Pocket157  label="Screwholes Servohorn Mount001"
  BaseFeature = -> Pocket158
  Length = 10
  Length2 = 100
  Profile = -> Sketch340
  Type = 0
FEATURE [PartDesign::Pocket] Pocket159  label="Bottom Nuthole Ball Bearing Mount (Interlock)"
  BaseFeature = -> Pocket157
  Length = 38
  Length2 = 100
  Profile = -> Sketch341
  Reversed = true
  Type = 0
FEATURE [PartDesign::Pocket] Pocket164  label="Top Nuthole Ball Bearing Mount (Interlock)"
  BaseFeature = -> Pocket159
  Length = 33
  Length2 = 100
  Profile = -> Sketch342
  Reversed = true
  Type = 0
FEATURE [Sketcher::SketchObject] Sketch344
  MapMode = 5
  Placement = pos=(0,10,-2.2e-15) rot=(1,0,0;1.5708rad)
  Support = -> [Pocket164]
  sketch-geometry (2):
    g0: Circle CenterX=121 CenterY=20 CenterZ=0 NormalX=0 NormalY=0 NormalZ=1 AngleXU=0 Radius=1.6
    g1: Circle CenterX=121 CenterY=10 CenterZ=0 NormalX=0 NormalY=0 NormalZ=1 AngleXU=0 Radius=1.6
  constraints (6):
    c: Vertical(g1,g0)
    c: Equal(g0,g1)
    c: Radius(g0) = 1.6
    c: DistanceY(g1,g0) = 10
    c: DistanceX(g-1,g1) = 121
    c: DistanceY(g-1,g1) = 10
FEATURE [PartDesign::Pocket] Pocket161  label="Screwholes Servopocket001"
  BaseFeature = -> Pocket164
  Length = 6
  Length2 = 100
  Profile = -> Sketch344
  Type = 0
FEATURE [Sketcher::SketchObject] Sketch345
  MapMode = 5
  Placement = pos=(0,0,25) rot=(1,0,0;3.14159rad)
  Support = -> [Pocket161]
  sketch-geometry (4):
    g0: LineSegment StartX=125 StartY=-26 StartZ=0 EndX=125 EndY=-34.5 EndZ=0
    g1: LineSegment StartX=125 StartY=-34.5 StartZ=0 EndX=30 EndY=-34.5 EndZ=0
    g2: LineSegment StartX=30 StartY=-26 StartZ=0 EndX=125 EndY=-26 EndZ=0
    g3: LineSegment StartX=30 StartY=-34.5 StartZ=0 EndX=30 EndY=-26 EndZ=0
  constraints (12):
    c: Coincident(g0,g1)
    c: Horizontal(g1)
    c: Vertical(g0)
    c: DistanceX(g-1,g0) = 125
    c: Coincident(g3,g2)
    c: Horizontal(g2)
    c: Vertical(g3)
    c: DistanceY(g3,g3) = 8.5
    c: DistanceY(g2,g-1) = 26
    c: DistanceX(g-1,g2) = 30
    c: Coincident(g3,g1)
    c: Coincident(g0,g2)
FEATURE [PartDesign::Pocket] Pocket162  label="Cableguide"
  BaseFeature = -> Pocket161
  Length = 2
  Length2 = 100
  Profile = -> Sketch345
  Type = 0
FEATURE [PartDesign::Fillet] Fillet056  label="Smooth Corners Cableguide"
  Base = -> Pocket162 [Edge183,Edge184,Edge188,Edge186]
  BaseFeature = -> Pocket162
  Radius = 1
FEATURE [PartDesign::Fillet] Fillet054  label="Smooth Interlock001"
  Base = -> Fillet056 [Edge89,Edge85,Edge79,Edge86,Edge78,Edge148,Edge80,Edge87,Edge27,Edge23,Edge25,Edge84]
  BaseFeature = -> Fillet056
  Radius = 0.2
FEATURE [Sketcher::SketchObject] Sketch346
  MapMode = 5
  Placement = pos=(130,0,0) rot=(0.57735,0.57735,0.57735;2.0944rad)
  Support = -> [Fillet054]
  sketch-geometry (9):
    g0: LineSegment StartX=30.75 StartY=19.75 StartZ=0 EndX=33.25 EndY=19.75 EndZ=0
    g1: LineSegment StartX=34.5 StartY=18.5 StartZ=0 EndX=34.5 EndY=11.5 EndZ=0
    g2: LineSegment StartX=33.25 StartY=10.25 StartZ=0 EndX=30.75 EndY=10.25 EndZ=0
    g3: LineSegment StartX=29.5 StartY=11.5 StartZ=0 EndX=29.5 EndY=18.5 EndZ=0
    g4: ArcOfCircle CenterX=30.75 CenterY=18.5 CenterZ=0 NormalX=0 NormalY=0 NormalZ=1 AngleXU=0 Radius=1.25 StartAngle=1.5708 EndAngle=3.14159
    g5: ArcOfCircle CenterX=33.25 CenterY=18.5 CenterZ=0 NormalX=0 NormalY=0 NormalZ=1 AngleXU=0 Radius=1.25 StartAngle=1e-16 EndAngle=1.5708
    g6: ArcOfCircle CenterX=33.25 CenterY=11.5 CenterZ=0 NormalX=0 NormalY=0 NormalZ=1 AngleXU=0 Radius=1.25 StartAngle=4.71239 EndAngle=6.28319
    g7: ArcOfCircle CenterX=30.75 CenterY=11.5 CenterZ=0 NormalX=0 NormalY=0 NormalZ=1 AngleXU=0 Radius=1.25 StartAngle=3.14159 EndAngle=4.71239
    g8: Circle [constr] CenterX=32 CenterY=15 CenterZ=0 NormalX=0 NormalY=0 NormalZ=1 AngleXU=0 Radius=2.5
  constraints (23):
    c: Horizontal(g0)
    c: Horizontal(g2)
    c: Vertical(g1)
    c: Vertical(g3)
    c: Tangent(g3,g4) = 1.5708
    c: Tangent(g0,g4) = 1.5708
    c: Tangent(g0,g5) = 1.5708
    c: Tangent(g1,g5) = 1.5708
    c: Tangent(g1,g6) = 1.5708
    c: Tangent(g2,g6) = 1.5708
    c: Tangent(g3,g7) = 1.5708
    c: Tangent(g2,g7) = 1.5708
    c: DistanceY(g2,g0) = 9.5
    c: DistanceX(g3,g1) = 5
    c: Tangent(g8,g3)
    c: Tangent(g8,g1)
    c: Equal(g5,g4)
    c: Equal(g4,g7)
    c: Equal(g7,g6)
    c: Radius(g5) = 1.25
    c: DistanceY(g8,g0) = 4.75
    c: DistanceX(g-1,g8) = 32
    c: DistanceY(g-1,g8) = 15
FEATURE [PartDesign::Pocket] Pocket163  label="Servocable001"
  BaseFeature = -> Fillet054
  Length = 5
  Length2 = 100
  Profile = -> Sketch346
  Type = 0
FEATURE [Sketcher::SketchObject] Sketch347
  MapMode = 5
  Placement = pos=(0,0,0) rot=(1,0,0;3.14159rad)
  Support = -> [Pocket163]
  sketch-geometry (4):
    g0: LineSegment StartX=117 StartY=-15 StartZ=0 EndX=125.25 EndY=-15 EndZ=0
    g1: LineSegment StartX=125.25 StartY=-15 StartZ=0 EndX=125.25 EndY=-10 EndZ=0
    g2: LineSegment StartX=125.25 StartY=-10 StartZ=0 EndX=117 EndY=-10 EndZ=0
    g3: LineSegment StartX=117 StartY=-10 StartZ=0 EndX=117 EndY=-15 EndZ=0
  constraints (12):
    c: Coincident(g0,g1)
    c: Coincident(g1,g2)
    c: Coincident(g2,g3)
    c: Coincident(g3,g0)
    c: Horizontal(g0)
    c: Horizontal(g2)
    c: Vertical(g1)
    c: Vertical(g3)
    c: DistanceX(g2,g2) = 8.25
    c: DistanceY(g3,g3) = 5
    c: DistanceY(g2,g-1) = 10
    c: DistanceX(g-1,g2) = 117
FEATURE [PartDesign::Pocket] Pocket165  label="Servopocket Interlock"
  BaseFeature = -> Pocket163
  Length = 5
  Length2 = 100
  Profile = -> Sketch347
  Type = 0
FEATURE [PartDesign::Body] Body061  label="Limb_Top_Shell"
  Group = -> [Sketch333,Pad117,Pocket154,Pocket153,Sketch334,SubtractivePipe005,Fillet058,Sketch332,Pocket152,Sketch335,Pocket155,Sketch337,Pocket156,Pad116,Fillet057,Sketch336,Pocket167,Fillet055,Sketch339,Pocket166,Sketch338,Pocket160,Sketch343,Pocket158,Sketch340,Pocket157,Sketch341,Pocket159,Sketch342,Pocket164,Sketch344,Pocket161,Sketch345,Pocket162,Fillet056,Fillet054,Sketch346,Pocket163,Sketch347,+1 more]
  Origin = -> Origin092
  Placement = pos=(-144.1,-29.45,42.1) rot=(0,0,1;0rad)
  Tip = -> Pocket165
FEATURE [PartDesign::Body] Body063
  Origin = -> Origin096
FEATURE [Sketcher::SketchObject] Sketch015
  MapMode = 5
  Support = -> [XY_Plane094]
  sketch-geometry (1):
    g0: Circle CenterX=0 CenterY=0 CenterZ=0 NormalX=0 NormalY=0 NormalZ=1 AngleXU=0 Radius=8
  constraints (2):
    c: Coincident(g0,g-1)
    c: Radius(g0) = 8
FEATURE [Sketcher::SketchObject] Sketch019
  MapMode = 5
  Support = -> [XY_Plane095]
  sketch-geometry (2):
    g0: Circle CenterX=0 CenterY=0 CenterZ=0 NormalX=0 NormalY=0 NormalZ=1 AngleXU=0 Radius=4
    g1: Circle CenterX=0 CenterY=0 CenterZ=0 NormalX=0 NormalY=0 NormalZ=1 AngleXU=0 Radius=6.25
  constraints (4):
    c: Coincident(g0,g-1)
    c: Coincident(g1,g0)
    c: Radius(g0) = 4
    c: Radius(g1) = 6.25
FEATURE [PartDesign::Pad] Pad009
  Length = 5
  Length2 = 100
  Profile = -> Sketch019
  Type = 0
FEATURE [PartDesign::Chamfer] Chamfer043
  Base = -> Pad009 [Face3,Face4]
  BaseFeature = -> Pad009
  Size = 0.2
FEATURE [PartDesign::Body] Body064
  Group = -> [Sketch019,Pad009,Chamfer043]
  Origin = -> Origin095
  Tip = -> Chamfer043
FEATURE [PartDesign::Pad] Pad008
  Length = 5
  Length2 = 100
  Profile = -> Sketch015
  Type = 0
FEATURE [Sketcher::SketchObject] Sketch016
  MapMode = 5
  Placement = pos=(0,0,0) rot=(1,0,0;3.14159rad)
  Support = -> [Pad008]
  sketch-geometry (1):
    g0: Circle CenterX=0 CenterY=0 CenterZ=0 NormalX=0 NormalY=0 NormalZ=1 AngleXU=0 Radius=2.5
  constraints (2):
    c: Coincident(g0,g-1)
    c: Radius(g0) = 2.5
FEATURE [PartDesign::Pocket] Pocket169
  BaseFeature = -> Pad008
  Length = 5
  Length2 = 100
  Profile = -> Sketch016
  Type = 0
FEATURE [Sketcher::SketchObject] Sketch017
  MapMode = 5
  Placement = pos=(0,0,0) rot=(1,0,0;3.14159rad)
  Support = -> [Pocket169]
  sketch-geometry (2):
    g0: Circle CenterX=0 CenterY=0 CenterZ=0 NormalX=0 NormalY=0 NormalZ=1 AngleXU=0 Radius=3.5
    g1: Circle CenterX=0 CenterY=0 CenterZ=0 NormalX=0 NormalY=0 NormalZ=1 AngleXU=0 Radius=7
  constraints (4):
    c: Coincident(g0,g-1)
    c: Coincident(g1,g0)
    c: Radius(g0) = 3.5
    c: Radius(g1) = 7
FEATURE [PartDesign::Pocket] Pocket170
  BaseFeature = -> Pocket169
  Length = 0.5
  Length2 = 100
  Profile = -> Sketch017
  Type = 0
FEATURE [Sketcher::SketchObject] Sketch018
  MapMode = 5
  Placement = pos=(0,0,5) rot=(0,0,1;0rad)
  Support = -> [Pocket170]
  sketch-geometry (2):
    g0: Circle CenterX=0 CenterY=0 CenterZ=0 NormalX=0 NormalY=0 NormalZ=1 AngleXU=0 Radius=3.5
    g1: Circle CenterX=0 CenterY=0 CenterZ=0 NormalX=0 NormalY=0 NormalZ=1 AngleXU=0 Radius=7
  constraints (4):
    c: Coincident(g0,g-1)
    c: Coincident(g1,g0)
    c: Radius(g0) = 3.5
    c: Radius(g1) = 7
FEATURE [PartDesign::Pocket] Pocket168
  BaseFeature = -> Pocket170
  Length = 0.5
  Length2 = 100
  Profile = -> Sketch018
  Type = 0
FEATURE [PartDesign::Chamfer] Chamfer042
  Base = -> Pocket168 [Face10,Face2,Face3,Face11]
  BaseFeature = -> Pocket168
  Size = 0.25
FEATURE [PartDesign::Body] Body062
  Group = -> [Sketch015,Pad008,Sketch016,Pocket169,Sketch017,Pocket170,Sketch018,Pocket168,Chamfer042]
  Origin = -> Origin094
  Tip = -> Chamfer042
FEATURE [App::Part] Part028  label="Ball Bearing"
  Group = -> [Body062,Body064,Body063]
  Origin = -> Origin007
  Placement = pos=(-144.1,26.5,26.95) rot=(1,0,0;1.5708rad)
FEATURE [Sketcher::SketchObject] Sketch348
  MapMode = 5
  Support = -> [XY_Plane097]
  sketch-geometry (8):
    g0: LineSegment StartX=0 StartY=3.17543 StartZ=0 EndX=-2.75 EndY=1.58771 EndZ=0
    g1: LineSegment StartX=-2.75 StartY=1.58771 StartZ=0 EndX=-2.75 EndY=-1.58771 EndZ=0
    g2: LineSegment StartX=-2.75 StartY=-1.58771 StartZ=0 EndX=0 EndY=-3.17543 EndZ=0
    g3: LineSegment StartX=0 StartY=-3.17543 StartZ=0 EndX=2.75 EndY=-1.58771 EndZ=0
    g4: LineSegment StartX=2.75 StartY=-1.58771 StartZ=0 EndX=2.75 EndY=1.58771 EndZ=0
    g5: LineSegment StartX=2.75 StartY=1.58771 StartZ=0 EndX=0 EndY=3.17543 EndZ=0
    g6: Circle [constr] CenterX=0 CenterY=0 CenterZ=0 NormalX=0 NormalY=0 NormalZ=1 AngleXU=0 Radius=3.17543
    g7: Circle CenterX=0 CenterY=0 CenterZ=0 NormalX=0 NormalY=0 NormalZ=1 AngleXU=0 Radius=1.5
  constraints (18):
    c: Coincident(g0,g1)
    c: Coincident(g1,g2)
    c: Coincident(g2,g3)
    c: Coincident(g3,g4)
    c: Coincident(g4,g5)
    c: Coincident(g5,g0)
    c: Equal(g0, g1-g5) x5
    c: PointOnObject(g0,g6)
    c: PointOnObject(g1,g6)
    c: PointOnObject(g2,g6)
    c: PointOnObject(g3,g6)
    c: PointOnObject(g4,g6)
    c: PointOnObject(g5,g6)
    c: Coincident(g6,g-1)
    c: PointOnObject(g5,g-2)
    c: DistanceX(g0,g4) = 5.5
    c: Coincident(g7,g-1)
    c: Radius(g7) = 1.5
FEATURE [PartDesign::Pad] Pad118  label="M3 Nut Primitive019"
  Length = 1.2
  Length2 = 1.2
  Profile = -> Sketch348
  Type = 4
FEATURE [Sketcher::SketchObject] Sketch349
  ExternalGeometry = -> [Pad118]
  MapMode = 5
  Placement = pos=(0,0,0) rot=(0.57735,0.57735,0.57735;2.0944rad)
  Support = -> [YZ_Plane097]
  sketch-geometry (6):
    g0: LineSegment StartX=-2.67543 StartY=1.2 StartZ=0 EndX=-3.67543 EndY=1.2 EndZ=0
    g1: LineSegment StartX=-3.67543 StartY=1.2 StartZ=0 EndX=-3.67543 EndY=-1.2 EndZ=0
    g2: LineSegment StartX=-3.67543 StartY=-1.2 StartZ=0 EndX=-2.67543 EndY=-1.2 EndZ=0
    g3: LineSegment StartX=-2.67543 StartY=-1.2 StartZ=0 EndX=-3.17543 EndY=-1 EndZ=0
    g4: LineSegment StartX=-3.17543 StartY=-1 StartZ=0 EndX=-3.17543 EndY=1 EndZ=0
    g5: LineSegment StartX=-3.17543 StartY=1 StartZ=0 EndX=-2.67543 EndY=1.2 EndZ=0
  constraints (15):
    c: Horizontal(g0)
    c: Coincident(g0,g1)
    c: Coincident(g1,g2)
    c: Coincident(g2,g3)
    c: Coincident(g3,g4)
    c: Coincident(g4,g5)
    c: Coincident(g5,g0)
    c: Symmetric(g4,g3,g-1)
    c: Symmetric(g0,g2,g-1)
    c: Symmetric(g1,g0,g-1)
    c: DistanceX(g0,g4) = 0.5
    c: DistanceY(g3,g4) = 2
    c: DistanceY(g1,g0) = 2.4
    c: PointOnObject(g3,g-3)
    c: DistanceX(g4,g0) = 0.5
FEATURE [PartDesign::Groove] Groove021  label="M3 Nut Smooth019"
  Angle = 360
  Axis = (-2e-16,3e-16,1)
  Base = (0,0,0)
  BaseFeature = -> Pad118
  Profile = -> Sketch349
  ReferenceAxis = -> Sketch349 [V_Axis]
  Reversed = true
FEATURE [PartDesign::Chamfer] Chamfer044  label="M3 Nut Smooth Hole019"
  Base = -> Groove021 [Edge24,Edge23]
  BaseFeature = -> Groove021
  Size = 0.2
FEATURE [PartDesign::Body] Body065  label="M3 Nut006"
  Group = -> [Sketch348,Pad118,Sketch349,Groove021,Chamfer044]
  Origin = -> Origin097
  Placement = pos=(-115.35,7.7,62.05) rot=(0.57735,0.57735,-0.57735;2.0944rad)
  Tip = -> Chamfer044
FEATURE [Sketcher::SketchObject] Sketch350
  MapMode = 5
  Support = -> [XY_Plane098]
  sketch-geometry (8):
    g0: LineSegment StartX=0 StartY=3.17543 StartZ=0 EndX=-2.75 EndY=1.58771 EndZ=0
    g1: LineSegment StartX=-2.75 StartY=1.58771 StartZ=0 EndX=-2.75 EndY=-1.58771 EndZ=0
    g2: LineSegment StartX=-2.75 StartY=-1.58771 StartZ=0 EndX=0 EndY=-3.17543 EndZ=0
    g3: LineSegment StartX=0 StartY=-3.17543 StartZ=0 EndX=2.75 EndY=-1.58771 EndZ=0
    g4: LineSegment StartX=2.75 StartY=-1.58771 StartZ=0 EndX=2.75 EndY=1.58771 EndZ=0
    g5: LineSegment StartX=2.75 StartY=1.58771 StartZ=0 EndX=0 EndY=3.17543 EndZ=0
    g6: Circle [constr] CenterX=0 CenterY=0 CenterZ=0 NormalX=0 NormalY=0 NormalZ=1 AngleXU=0 Radius=3.17543
    g7: Circle CenterX=0 CenterY=0 CenterZ=0 NormalX=0 NormalY=0 NormalZ=1 AngleXU=0 Radius=1.5
  constraints (18):
    c: Coincident(g0,g1)
    c: Coincident(g1,g2)
    c: Coincident(g2,g3)
    c: Coincident(g3,g4)
    c: Coincident(g4,g5)
    c: Coincident(g5,g0)
    c: Equal(g0, g1-g5) x5
    c: PointOnObject(g0,g6)
    c: PointOnObject(g1,g6)
    c: PointOnObject(g2,g6)
    c: PointOnObject(g3,g6)
    c: PointOnObject(g4,g6)
    c: PointOnObject(g5,g6)
    c: Coincident(g6,g-1)
    c: PointOnObject(g5,g-2)
    c: DistanceX(g0,g4) = 5.5
    c: Coincident(g7,g-1)
    c: Radius(g7) = 1.5
FEATURE [PartDesign::Pad] Pad119  label="M3 Nut Primitive020"
  Length = 1.2
  Length2 = 1.2
  Profile = -> Sketch350
  Type = 4
FEATURE [Sketcher::SketchObject] Sketch351
  ExternalGeometry = -> [Pad119]
  MapMode = 5
  Placement = pos=(0,0,0) rot=(0.57735,0.57735,0.57735;2.0944rad)
  Support = -> [YZ_Plane098]
  sketch-geometry (6):
    g0: LineSegment StartX=-2.67543 StartY=1.2 StartZ=0 EndX=-3.67543 EndY=1.2 EndZ=0
    g1: LineSegment StartX=-3.67543 StartY=1.2 StartZ=0 EndX=-3.67543 EndY=-1.2 EndZ=0
    g2: LineSegment StartX=-3.67543 StartY=-1.2 StartZ=0 EndX=-2.67543 EndY=-1.2 EndZ=0
    g3: LineSegment StartX=-2.67543 StartY=-1.2 StartZ=0 EndX=-3.17543 EndY=-1 EndZ=0
    g4: LineSegment StartX=-3.17543 StartY=-1 StartZ=0 EndX=-3.17543 EndY=1 EndZ=0
    g5: LineSegment StartX=-3.17543 StartY=1 StartZ=0 EndX=-2.67543 EndY=1.2 EndZ=0
  constraints (15):
    c: Horizontal(g0)
    c: Coincident(g0,g1)
    c: Coincident(g1,g2)
    c: Coincident(g2,g3)
    c: Coincident(g3,g4)
    c: Coincident(g4,g5)
    c: Coincident(g5,g0)
    c: Symmetric(g4,g3,g-1)
    c: Symmetric(g0,g2,g-1)
    c: Symmetric(g1,g0,g-1)
    c: DistanceX(g0,g4) = 0.5
    c: DistanceY(g3,g4) = 2
    c: DistanceY(g1,g0) = 2.4
    c: PointOnObject(g3,g-3)
    c: DistanceX(g4,g0) = 0.5
FEATURE [PartDesign::Groove] Groove022  label="M3 Nut Smooth020"
  Angle = 360
  Axis = (-2e-16,3e-16,1)
  Base = (0,0,0)
  BaseFeature = -> Pad119
  Profile = -> Sketch351
  ReferenceAxis = -> Sketch351 [V_Axis]
  Reversed = true
FEATURE [PartDesign::Chamfer] Chamfer045  label="M3 Nut Smooth Hole020"
  Base = -> Groove022 [Edge24,Edge23]
  BaseFeature = -> Groove022
  Size = 0.2
FEATURE [PartDesign::Body] Body066  label="M3 Nut007"
  Group = -> [Sketch350,Pad119,Sketch351,Groove022,Chamfer045]
  Origin = -> Origin098
  Placement = pos=(-110.55,7.7,52.05) rot=(0.57735,0.57735,-0.57735;2.0944rad)
  Tip = -> Chamfer045
FEATURE [Sketcher::SketchObject] Sketch352
  MapMode = 5
  Support = -> [XY_Plane099]
  sketch-geometry (8):
    g0: LineSegment StartX=0 StartY=3.17543 StartZ=0 EndX=-2.75 EndY=1.58771 EndZ=0
    g1: LineSegment StartX=-2.75 StartY=1.58771 StartZ=0 EndX=-2.75 EndY=-1.58771 EndZ=0
    g2: LineSegment StartX=-2.75 StartY=-1.58771 StartZ=0 EndX=0 EndY=-3.17543 EndZ=0
    g3: LineSegment StartX=0 StartY=-3.17543 StartZ=0 EndX=2.75 EndY=-1.58771 EndZ=0
    g4: LineSegment StartX=2.75 StartY=-1.58771 StartZ=0 EndX=2.75 EndY=1.58771 EndZ=0
    g5: LineSegment StartX=2.75 StartY=1.58771 StartZ=0 EndX=0 EndY=3.17543 EndZ=0
    g6: Circle [constr] CenterX=0 CenterY=0 CenterZ=0 NormalX=0 NormalY=0 NormalZ=1 AngleXU=0 Radius=3.17543
    g7: Circle CenterX=0 CenterY=0 CenterZ=0 NormalX=0 NormalY=0 NormalZ=1 AngleXU=0 Radius=1.5
  constraints (18):
    c: Coincident(g0,g1)
    c: Coincident(g1,g2)
    c: Coincident(g2,g3)
    c: Coincident(g3,g4)
    c: Coincident(g4,g5)
    c: Coincident(g5,g0)
    c: Equal(g0, g1-g5) x5
    c: PointOnObject(g0,g6)
    c: PointOnObject(g1,g6)
    c: PointOnObject(g2,g6)
    c: PointOnObject(g3,g6)
    c: PointOnObject(g4,g6)
    c: PointOnObject(g5,g6)
    c: Coincident(g6,g-1)
    c: PointOnObject(g5,g-2)
    c: DistanceX(g0,g4) = 5.5
    c: Coincident(g7,g-1)
    c: Radius(g7) = 1.5
FEATURE [PartDesign::Pad] Pad120  label="M3 Nut Primitive021"
  Length = 1.2
  Length2 = 1.2
  Profile = -> Sketch352
  Type = 4
FEATURE [Sketcher::SketchObject] Sketch353
  ExternalGeometry = -> [Pad120]
  MapMode = 5
  Placement = pos=(0,0,0) rot=(0.57735,0.57735,0.57735;2.0944rad)
  Support = -> [YZ_Plane099]
  sketch-geometry (6):
    g0: LineSegment StartX=-2.67543 StartY=1.2 StartZ=0 EndX=-3.67543 EndY=1.2 EndZ=0
    g1: LineSegment StartX=-3.67543 StartY=1.2 StartZ=0 EndX=-3.67543 EndY=-1.2 EndZ=0
    g2: LineSegment StartX=-3.67543 StartY=-1.2 StartZ=0 EndX=-2.67543 EndY=-1.2 EndZ=0
    g3: LineSegment StartX=-2.67543 StartY=-1.2 StartZ=0 EndX=-3.17543 EndY=-1 EndZ=0
    g4: LineSegment StartX=-3.17543 StartY=-1 StartZ=0 EndX=-3.17543 EndY=1 EndZ=0
    g5: LineSegment StartX=-3.17543 StartY=1 StartZ=0 EndX=-2.67543 EndY=1.2 EndZ=0
  constraints (15):
    c: Horizontal(g0)
    c: Coincident(g0,g1)
    c: Coincident(g1,g2)
    c: Coincident(g2,g3)
    c: Coincident(g3,g4)
    c: Coincident(g4,g5)
    c: Coincident(g5,g0)
    c: Symmetric(g4,g3,g-1)
    c: Symmetric(g0,g2,g-1)
    c: Symmetric(g1,g0,g-1)
    c: DistanceX(g0,g4) = 0.5
    c: DistanceY(g3,g4) = 2
    c: DistanceY(g1,g0) = 2.4
    c: PointOnObject(g3,g-3)
    c: DistanceX(g4,g0) = 0.5
FEATURE [PartDesign::Groove] Groove023  label="M3 Nut Smooth021"
  Angle = 360
  Axis = (-2e-16,3e-16,1)
  Base = (0,0,0)
  BaseFeature = -> Pad120
  Profile = -> Sketch353
  ReferenceAxis = -> Sketch353 [V_Axis]
  Reversed = true
FEATURE [PartDesign::Chamfer] Chamfer046  label="M3 Nut Smooth Hole021"
  Base = -> Groove023 [Edge24,Edge23]
  BaseFeature = -> Groove023
  Size = 0.2
FEATURE [PartDesign::Body] Body067  label="M3 Nut008"
  Group = -> [Sketch352,Pad120,Sketch353,Groove023,Chamfer046]
  Origin = -> Origin099
  Placement = pos=(-115.35,-9.3,62.1) rot=(0.57735,0.57735,-0.57735;2.0944rad)
  Tip = -> Chamfer046
FEATURE [Sketcher::SketchObject] Sketch354
  MapMode = 5
  Support = -> [XY_Plane100]
  sketch-geometry (8):
    g0: LineSegment StartX=0 StartY=3.17543 StartZ=0 EndX=-2.75 EndY=1.58771 EndZ=0
    g1: LineSegment StartX=-2.75 StartY=1.58771 StartZ=0 EndX=-2.75 EndY=-1.58771 EndZ=0
    g2: LineSegment StartX=-2.75 StartY=-1.58771 StartZ=0 EndX=0 EndY=-3.17543 EndZ=0
    g3: LineSegment StartX=0 StartY=-3.17543 StartZ=0 EndX=2.75 EndY=-1.58771 EndZ=0
    g4: LineSegment StartX=2.75 StartY=-1.58771 StartZ=0 EndX=2.75 EndY=1.58771 EndZ=0
    g5: LineSegment StartX=2.75 StartY=1.58771 StartZ=0 EndX=0 EndY=3.17543 EndZ=0
    g6: Circle [constr] CenterX=0 CenterY=0 CenterZ=0 NormalX=0 NormalY=0 NormalZ=1 AngleXU=0 Radius=3.17543
    g7: Circle CenterX=0 CenterY=0 CenterZ=0 NormalX=0 NormalY=0 NormalZ=1 AngleXU=0 Radius=1.5
  constraints (18):
    c: Coincident(g0,g1)
    c: Coincident(g1,g2)
    c: Coincident(g2,g3)
    c: Coincident(g3,g4)
    c: Coincident(g4,g5)
    c: Coincident(g5,g0)
    c: Equal(g0, g1-g5) x5
    c: PointOnObject(g0,g6)
    c: PointOnObject(g1,g6)
    c: PointOnObject(g2,g6)
    c: PointOnObject(g3,g6)
    c: PointOnObject(g4,g6)
    c: PointOnObject(g5,g6)
    c: Coincident(g6,g-1)
    c: PointOnObject(g5,g-2)
    c: DistanceX(g0,g4) = 5.5
    c: Coincident(g7,g-1)
    c: Radius(g7) = 1.5
FEATURE [PartDesign::Pad] Pad121  label="M3 Nut Primitive022"
  Length = 1.2
  Length2 = 1.2
  Profile = -> Sketch354
  Type = 4
FEATURE [Sketcher::SketchObject] Sketch355
  ExternalGeometry = -> [Pad121]
  MapMode = 5
  Placement = pos=(0,0,0) rot=(0.57735,0.57735,0.57735;2.0944rad)
  Support = -> [YZ_Plane100]
  sketch-geometry (6):
    g0: LineSegment StartX=-2.67543 StartY=1.2 StartZ=0 EndX=-3.67543 EndY=1.2 EndZ=0
    g1: LineSegment StartX=-3.67543 StartY=1.2 StartZ=0 EndX=-3.67543 EndY=-1.2 EndZ=0
    g2: LineSegment StartX=-3.67543 StartY=-1.2 StartZ=0 EndX=-2.67543 EndY=-1.2 EndZ=0
    g3: LineSegment StartX=-2.67543 StartY=-1.2 StartZ=0 EndX=-3.17543 EndY=-1 EndZ=0
    g4: LineSegment StartX=-3.17543 StartY=-1 StartZ=0 EndX=-3.17543 EndY=1 EndZ=0
    g5: LineSegment StartX=-3.17543 StartY=1 StartZ=0 EndX=-2.67543 EndY=1.2 EndZ=0
  constraints (15):
    c: Horizontal(g0)
    c: Coincident(g0,g1)
    c: Coincident(g1,g2)
    c: Coincident(g2,g3)
    c: Coincident(g3,g4)
    c: Coincident(g4,g5)
    c: Coincident(g5,g0)
    c: Symmetric(g4,g3,g-1)
    c: Symmetric(g0,g2,g-1)
    c: Symmetric(g1,g0,g-1)
    c: DistanceX(g0,g4) = 0.5
    c: DistanceY(g3,g4) = 2
    c: DistanceY(g1,g0) = 2.4
    c: PointOnObject(g3,g-3)
    c: DistanceX(g4,g0) = 0.5
FEATURE [PartDesign::Groove] Groove024  label="M3 Nut Smooth022"
  Angle = 360
  Axis = (-2e-16,3e-16,1)
  Base = (0,0,0)
  BaseFeature = -> Pad121
  Profile = -> Sketch355
  ReferenceAxis = -> Sketch355 [V_Axis]
  Reversed = true
FEATURE [PartDesign::Chamfer] Chamfer047  label="M3 Nut Smooth Hole022"
  Base = -> Groove024 [Edge24,Edge23]
  BaseFeature = -> Groove024
  Size = 0.2
FEATURE [PartDesign::Body] Body068  label="M3 Nut009"
  Group = -> [Sketch354,Pad121,Sketch355,Groove024,Chamfer047]
  Origin = -> Origin100
  Placement = pos=(-110.6,-9.3,52.1) rot=(0.57735,0.57735,-0.57735;2.0944rad)
  Tip = -> Chamfer047
FEATURE [Sketcher::SketchObject] Sketch356
  MapMode = 5
  Support = -> [XY_Plane101]
  sketch-geometry (8):
    g0: LineSegment StartX=0 StartY=3.17543 StartZ=0 EndX=-2.75 EndY=1.58771 EndZ=0
    g1: LineSegment StartX=-2.75 StartY=1.58771 StartZ=0 EndX=-2.75 EndY=-1.58771 EndZ=0
    g2: LineSegment StartX=-2.75 StartY=-1.58771 StartZ=0 EndX=0 EndY=-3.17543 EndZ=0
    g3: LineSegment StartX=0 StartY=-3.17543 StartZ=0 EndX=2.75 EndY=-1.58771 EndZ=0
    g4: LineSegment StartX=2.75 StartY=-1.58771 StartZ=0 EndX=2.75 EndY=1.58771 EndZ=0
    g5: LineSegment StartX=2.75 StartY=1.58771 StartZ=0 EndX=0 EndY=3.17543 EndZ=0
    g6: Circle [constr] CenterX=0 CenterY=0 CenterZ=0 NormalX=0 NormalY=0 NormalZ=1 AngleXU=0 Radius=3.17543
    g7: Circle CenterX=0 CenterY=0 CenterZ=0 NormalX=0 NormalY=0 NormalZ=1 AngleXU=0 Radius=1.5
  constraints (18):
    c: Coincident(g0,g1)
    c: Coincident(g1,g2)
    c: Coincident(g2,g3)
    c: Coincident(g3,g4)
    c: Coincident(g4,g5)
    c: Coincident(g5,g0)
    c: Equal(g0, g1-g5) x5
    c: PointOnObject(g0,g6)
    c: PointOnObject(g1,g6)
    c: PointOnObject(g2,g6)
    c: PointOnObject(g3,g6)
    c: PointOnObject(g4,g6)
    c: PointOnObject(g5,g6)
    c: Coincident(g6,g-1)
    c: PointOnObject(g5,g-2)
    c: DistanceX(g0,g4) = 5.5
    c: Coincident(g7,g-1)
    c: Radius(g7) = 1.5
FEATURE [PartDesign::Pad] Pad122  label="M3 Nut Primitive023"
  Length = 1.2
  Length2 = 1.2
  Profile = -> Sketch356
  Type = 4
FEATURE [Sketcher::SketchObject] Sketch357
  ExternalGeometry = -> [Pad122]
  MapMode = 5
  Placement = pos=(0,0,0) rot=(0.57735,0.57735,0.57735;2.0944rad)
  Support = -> [YZ_Plane101]
  sketch-geometry (6):
    g0: LineSegment StartX=-2.67543 StartY=1.2 StartZ=0 EndX=-3.67543 EndY=1.2 EndZ=0
    g1: LineSegment StartX=-3.67543 StartY=1.2 StartZ=0 EndX=-3.67543 EndY=-1.2 EndZ=0
    g2: LineSegment StartX=-3.67543 StartY=-1.2 StartZ=0 EndX=-2.67543 EndY=-1.2 EndZ=0
    g3: LineSegment StartX=-2.67543 StartY=-1.2 StartZ=0 EndX=-3.17543 EndY=-1 EndZ=0
    g4: LineSegment StartX=-3.17543 StartY=-1 StartZ=0 EndX=-3.17543 EndY=1 EndZ=0
    g5: LineSegment StartX=-3.17543 StartY=1 StartZ=0 EndX=-2.67543 EndY=1.2 EndZ=0
  constraints (15):
    c: Horizontal(g0)
    c: Coincident(g0,g1)
    c: Coincident(g1,g2)
    c: Coincident(g2,g3)
    c: Coincident(g3,g4)
    c: Coincident(g4,g5)
    c: Coincident(g5,g0)
    c: Symmetric(g4,g3,g-1)
    c: Symmetric(g0,g2,g-1)
    c: Symmetric(g1,g0,g-1)
    c: DistanceX(g0,g4) = 0.5
    c: DistanceY(g3,g4) = 2
    c: DistanceY(g1,g0) = 2.4
    c: PointOnObject(g3,g-3)
    c: DistanceX(g4,g0) = 0.5
FEATURE [PartDesign::Groove] Groove025  label="M3 Nut Smooth023"
  Angle = 360
  Axis = (-2e-16,3e-16,1)
  Base = (0,0,0)
  BaseFeature = -> Pad122
  Profile = -> Sketch357
  ReferenceAxis = -> Sketch357 [V_Axis]
  Reversed = true
FEATURE [PartDesign::Chamfer] Chamfer048  label="M3 Nut Smooth Hole023"
  Base = -> Groove025 [Edge24,Edge23]
  BaseFeature = -> Groove025
  Size = 0.2
FEATURE [PartDesign::Body] Body069  label="M3 Nut010"
  Group = -> [Sketch356,Pad122,Sketch357,Groove025,Chamfer048]
  Origin = -> Origin101
  Placement = pos=(-71.5,-9.8,62.05) rot=(0.57735,-0.57735,0.57735;2.0944rad)
  Tip = -> Chamfer048
FEATURE [Sketcher::SketchObject] Sketch358
  MapMode = 5
  Support = -> [XY_Plane102]
  sketch-geometry (8):
    g0: LineSegment StartX=0 StartY=3.17543 StartZ=0 EndX=-2.75 EndY=1.58771 EndZ=0
    g1: LineSegment StartX=-2.75 StartY=1.58771 StartZ=0 EndX=-2.75 EndY=-1.58771 EndZ=0
    g2: LineSegment StartX=-2.75 StartY=-1.58771 StartZ=0 EndX=0 EndY=-3.17543 EndZ=0
    g3: LineSegment StartX=0 StartY=-3.17543 StartZ=0 EndX=2.75 EndY=-1.58771 EndZ=0
    g4: LineSegment StartX=2.75 StartY=-1.58771 StartZ=0 EndX=2.75 EndY=1.58771 EndZ=0
    g5: LineSegment StartX=2.75 StartY=1.58771 StartZ=0 EndX=0 EndY=3.17543 EndZ=0
    g6: Circle [constr] CenterX=0 CenterY=0 CenterZ=0 NormalX=0 NormalY=0 NormalZ=1 AngleXU=0 Radius=3.17543
    g7: Circle CenterX=0 CenterY=0 CenterZ=0 NormalX=0 NormalY=0 NormalZ=1 AngleXU=0 Radius=1.5
  constraints (18):
    c: Coincident(g0,g1)
    c: Coincident(g1,g2)
    c: Coincident(g2,g3)
    c: Coincident(g3,g4)
    c: Coincident(g4,g5)
    c: Coincident(g5,g0)
    c: Equal(g0, g1-g5) x5
    c: PointOnObject(g0,g6)
    c: PointOnObject(g1,g6)
    c: PointOnObject(g2,g6)
    c: PointOnObject(g3,g6)
    c: PointOnObject(g4,g6)
    c: PointOnObject(g5,g6)
    c: Coincident(g6,g-1)
    c: PointOnObject(g5,g-2)
    c: DistanceX(g0,g4) = 5.5
    c: Coincident(g7,g-1)
    c: Radius(g7) = 1.5
FEATURE [PartDesign::Pad] Pad123  label="M3 Nut Primitive024"
  Length = 1.2
  Length2 = 1.2
  Profile = -> Sketch358
  Type = 4
FEATURE [Sketcher::SketchObject] Sketch359
  ExternalGeometry = -> [Pad123]
  MapMode = 5
  Placement = pos=(0,0,0) rot=(0.57735,0.57735,0.57735;2.0944rad)
  Support = -> [YZ_Plane102]
  sketch-geometry (6):
    g0: LineSegment StartX=-2.67543 StartY=1.2 StartZ=0 EndX=-3.67543 EndY=1.2 EndZ=0
    g1: LineSegment StartX=-3.67543 StartY=1.2 StartZ=0 EndX=-3.67543 EndY=-1.2 EndZ=0
    g2: LineSegment StartX=-3.67543 StartY=-1.2 StartZ=0 EndX=-2.67543 EndY=-1.2 EndZ=0
    g3: LineSegment StartX=-2.67543 StartY=-1.2 StartZ=0 EndX=-3.17543 EndY=-1 EndZ=0
    g4: LineSegment StartX=-3.17543 StartY=-1 StartZ=0 EndX=-3.17543 EndY=1 EndZ=0
    g5: LineSegment StartX=-3.17543 StartY=1 StartZ=0 EndX=-2.67543 EndY=1.2 EndZ=0
  constraints (15):
    c: Horizontal(g0)
    c: Coincident(g0,g1)
    c: Coincident(g1,g2)
    c: Coincident(g2,g3)
    c: Coincident(g3,g4)
    c: Coincident(g4,g5)
    c: Coincident(g5,g0)
    c: Symmetric(g4,g3,g-1)
    c: Symmetric(g0,g2,g-1)
    c: Symmetric(g1,g0,g-1)
    c: DistanceX(g0,g4) = 0.5
    c: DistanceY(g3,g4) = 2
    c: DistanceY(g1,g0) = 2.4
    c: PointOnObject(g3,g-3)
    c: DistanceX(g4,g0) = 0.5
FEATURE [PartDesign::Groove] Groove026  label="M3 Nut Smooth024"
  Angle = 360
  Axis = (-2e-16,3e-16,1)
  Base = (0,0,0)
  BaseFeature = -> Pad123
  Profile = -> Sketch359
  ReferenceAxis = -> Sketch359 [V_Axis]
  Reversed = true
FEATURE [PartDesign::Chamfer] Chamfer049  label="M3 Nut Smooth Hole024"
  Base = -> Groove026 [Edge24,Edge23]
  BaseFeature = -> Groove026
  Size = 0.2
FEATURE [PartDesign::Body] Body070  label="M3 Nut011"
  Group = -> [Sketch358,Pad123,Sketch359,Groove026,Chamfer049]
  Origin = -> Origin102
  Placement = pos=(-23,-9.8,62.05) rot=(0.57735,-0.57735,0.57735;2.0944rad)
  Tip = -> Chamfer049
FEATURE [Sketcher::SketchObject] Sketch360
  MapMode = 5
  Support = -> [XY_Plane103]
  sketch-geometry (8):
    g0: LineSegment StartX=0 StartY=3.17543 StartZ=0 EndX=-2.75 EndY=1.58771 EndZ=0
    g1: LineSegment StartX=-2.75 StartY=1.58771 StartZ=0 EndX=-2.75 EndY=-1.58771 EndZ=0
    g2: LineSegment StartX=-2.75 StartY=-1.58771 StartZ=0 EndX=0 EndY=-3.17543 EndZ=0
    g3: LineSegment StartX=0 StartY=-3.17543 StartZ=0 EndX=2.75 EndY=-1.58771 EndZ=0
    g4: LineSegment StartX=2.75 StartY=-1.58771 StartZ=0 EndX=2.75 EndY=1.58771 EndZ=0
    g5: LineSegment StartX=2.75 StartY=1.58771 StartZ=0 EndX=0 EndY=3.17543 EndZ=0
    g6: Circle [constr] CenterX=0 CenterY=0 CenterZ=0 NormalX=0 NormalY=0 NormalZ=1 AngleXU=0 Radius=3.17543
    g7: Circle CenterX=0 CenterY=0 CenterZ=0 NormalX=0 NormalY=0 NormalZ=1 AngleXU=0 Radius=1.5
  constraints (18):
    c: Coincident(g0,g1)
    c: Coincident(g1,g2)
    c: Coincident(g2,g3)
    c: Coincident(g3,g4)
    c: Coincident(g4,g5)
    c: Coincident(g5,g0)
    c: Equal(g0, g1-g5) x5
    c: PointOnObject(g0,g6)
    c: PointOnObject(g1,g6)
    c: PointOnObject(g2,g6)
    c: PointOnObject(g3,g6)
    c: PointOnObject(g4,g6)
    c: PointOnObject(g5,g6)
    c: Coincident(g6,g-1)
    c: PointOnObject(g5,g-2)
    c: DistanceX(g0,g4) = 5.5
    c: Coincident(g7,g-1)
    c: Radius(g7) = 1.5
FEATURE [PartDesign::Pad] Pad124  label="M3 Nut Primitive025"
  Length = 1.2
  Length2 = 1.2
  Profile = -> Sketch360
  Type = 4
FEATURE [Sketcher::SketchObject] Sketch361
  ExternalGeometry = -> [Pad124]
  MapMode = 5
  Placement = pos=(0,0,0) rot=(0.57735,0.57735,0.57735;2.0944rad)
  Support = -> [YZ_Plane103]
  sketch-geometry (6):
    g0: LineSegment StartX=-2.67543 StartY=1.2 StartZ=0 EndX=-3.67543 EndY=1.2 EndZ=0
    g1: LineSegment StartX=-3.67543 StartY=1.2 StartZ=0 EndX=-3.67543 EndY=-1.2 EndZ=0
    g2: LineSegment StartX=-3.67543 StartY=-1.2 StartZ=0 EndX=-2.67543 EndY=-1.2 EndZ=0
    g3: LineSegment StartX=-2.67543 StartY=-1.2 StartZ=0 EndX=-3.17543 EndY=-1 EndZ=0
    g4: LineSegment StartX=-3.17543 StartY=-1 StartZ=0 EndX=-3.17543 EndY=1 EndZ=0
    g5: LineSegment StartX=-3.17543 StartY=1 StartZ=0 EndX=-2.67543 EndY=1.2 EndZ=0
  constraints (15):
    c: Horizontal(g0)
    c: Coincident(g0,g1)
    c: Coincident(g1,g2)
    c: Coincident(g2,g3)
    c: Coincident(g3,g4)
    c: Coincident(g4,g5)
    c: Coincident(g5,g0)
    c: Symmetric(g4,g3,g-1)
    c: Symmetric(g0,g2,g-1)
    c: Symmetric(g1,g0,g-1)
    c: DistanceX(g0,g4) = 0.5
    c: DistanceY(g3,g4) = 2
    c: DistanceY(g1,g0) = 2.4
    c: PointOnObject(g3,g-3)
    c: DistanceX(g4,g0) = 0.5
FEATURE [PartDesign::Groove] Groove027  label="M3 Nut Smooth025"
  Angle = 360
  Axis = (-2e-16,3e-16,1)
  Base = (0,0,0)
  BaseFeature = -> Pad124
  Profile = -> Sketch361
  ReferenceAxis = -> Sketch361 [V_Axis]
  Reversed = true
FEATURE [PartDesign::Chamfer] Chamfer050  label="M3 Nut Smooth Hole025"
  Base = -> Groove027 [Edge24,Edge23]
  BaseFeature = -> Groove027
  Size = 0.2
FEATURE [PartDesign::Body] Body071  label="M3 Nut012"
  Group = -> [Sketch360,Pad124,Sketch361,Groove027,Chamfer050]
  Origin = -> Origin103
  Placement = pos=(-71.6,-9.85,52.05) rot=(0.57735,-0.57735,0.57735;2.0944rad)
  Tip = -> Chamfer050
FEATURE [Sketcher::SketchObject] Sketch362
  MapMode = 5
  Support = -> [XY_Plane104]
  sketch-geometry (8):
    g0: LineSegment StartX=0 StartY=3.17543 StartZ=0 EndX=-2.75 EndY=1.58771 EndZ=0
    g1: LineSegment StartX=-2.75 StartY=1.58771 StartZ=0 EndX=-2.75 EndY=-1.58771 EndZ=0
    g2: LineSegment StartX=-2.75 StartY=-1.58771 StartZ=0 EndX=0 EndY=-3.17543 EndZ=0
    g3: LineSegment StartX=0 StartY=-3.17543 StartZ=0 EndX=2.75 EndY=-1.58771 EndZ=0
    g4: LineSegment StartX=2.75 StartY=-1.58771 StartZ=0 EndX=2.75 EndY=1.58771 EndZ=0
    g5: LineSegment StartX=2.75 StartY=1.58771 StartZ=0 EndX=0 EndY=3.17543 EndZ=0
    g6: Circle [constr] CenterX=0 CenterY=0 CenterZ=0 NormalX=0 NormalY=0 NormalZ=1 AngleXU=0 Radius=3.17543
    g7: Circle CenterX=0 CenterY=0 CenterZ=0 NormalX=0 NormalY=0 NormalZ=1 AngleXU=0 Radius=1.5
  constraints (18):
    c: Coincident(g0,g1)
    c: Coincident(g1,g2)
    c: Coincident(g2,g3)
    c: Coincident(g3,g4)
    c: Coincident(g4,g5)
    c: Coincident(g5,g0)
    c: Equal(g0, g1-g5) x5
    c: PointOnObject(g0,g6)
    c: PointOnObject(g1,g6)
    c: PointOnObject(g2,g6)
    c: PointOnObject(g3,g6)
    c: PointOnObject(g4,g6)
    c: PointOnObject(g5,g6)
    c: Coincident(g6,g-1)
    c: PointOnObject(g5,g-2)
    c: DistanceX(g0,g4) = 5.5
    c: Coincident(g7,g-1)
    c: Radius(g7) = 1.5
FEATURE [PartDesign::Pad] Pad125  label="M3 Nut Primitive026"
  Length = 1.2
  Length2 = 1.2
  Profile = -> Sketch362
  Type = 4
FEATURE [Sketcher::SketchObject] Sketch363
  ExternalGeometry = -> [Pad125]
  MapMode = 5
  Placement = pos=(0,0,0) rot=(0.57735,0.57735,0.57735;2.0944rad)
  Support = -> [YZ_Plane104]
  sketch-geometry (6):
    g0: LineSegment StartX=-2.67543 StartY=1.2 StartZ=0 EndX=-3.67543 EndY=1.2 EndZ=0
    g1: LineSegment StartX=-3.67543 StartY=1.2 StartZ=0 EndX=-3.67543 EndY=-1.2 EndZ=0
    g2: LineSegment StartX=-3.67543 StartY=-1.2 StartZ=0 EndX=-2.67543 EndY=-1.2 EndZ=0
    g3: LineSegment StartX=-2.67543 StartY=-1.2 StartZ=0 EndX=-3.17543 EndY=-1 EndZ=0
    g4: LineSegment StartX=-3.17543 StartY=-1 StartZ=0 EndX=-3.17543 EndY=1 EndZ=0
    g5: LineSegment StartX=-3.17543 StartY=1 StartZ=0 EndX=-2.67543 EndY=1.2 EndZ=0
  constraints (15):
    c: Horizontal(g0)
    c: Coincident(g0,g1)
    c: Coincident(g1,g2)
    c: Coincident(g2,g3)
    c: Coincident(g3,g4)
    c: Coincident(g4,g5)
    c: Coincident(g5,g0)
    c: Symmetric(g4,g3,g-1)
    c: Symmetric(g0,g2,g-1)
    c: Symmetric(g1,g0,g-1)
    c: DistanceX(g0,g4) = 0.5
    c: DistanceY(g3,g4) = 2
    c: DistanceY(g1,g0) = 2.4
    c: PointOnObject(g3,g-3)
    c: DistanceX(g4,g0) = 0.5
FEATURE [PartDesign::Groove] Groove028  label="M3 Nut Smooth026"
  Angle = 360
  Axis = (-2e-16,3e-16,1)
  Base = (0,0,0)
  BaseFeature = -> Pad125
  Profile = -> Sketch363
  ReferenceAxis = -> Sketch363 [V_Axis]
  Reversed = true
FEATURE [PartDesign::Chamfer] Chamfer051  label="M3 Nut Smooth Hole026"
  Base = -> Groove028 [Edge24,Edge23]
  BaseFeature = -> Groove028
  Size = 0.2
FEATURE [PartDesign::Body] Body072  label="M3 Nut013"
  Group = -> [Sketch362,Pad125,Sketch363,Groove028,Chamfer051]
  Origin = -> Origin104
  Placement = pos=(-23.1,-9.85,52.05) rot=(0.57735,-0.57735,0.57735;2.0944rad)
  Tip = -> Chamfer051
FEATURE [App::Part] Part029  label="Shell Nuts"
  Group = -> [Body065,Body066,Body067,Body068]
  Origin = -> Origin105
FEATURE [App::Part] Part030  label="Servo Nuts"
  Group = -> [Body069,Body070,Body071,Body072]
  Origin = -> Origin106
FEATURE [Sketcher::SketchObject] Sketch377
  MapMode = 5
  Placement = pos=(0,0,0) rot=(1,0,0;1.5708rad)
  Support = -> [XZ_Plane108]
  sketch-geometry (1):
    g0: Circle CenterX=1.55 CenterY=4 CenterZ=0 NormalX=0 NormalY=0 NormalZ=1 AngleXU=0 Radius=0.75
  constraints (3):
    c: Radius(g0) = 0.75
    c: DistanceY(g-1,g0) = 4
    c: DistanceX(g-1,g0) = 1.55
FEATURE [Sketcher::SketchObject] Sketch379
  MapMode = 5
  Support = -> [XY_Plane107]
  sketch-geometry (4):
    g0: LineSegment StartX=-10 StartY=20.15 StartZ=0 EndX=10 EndY=20.15 EndZ=0
    g1: LineSegment StartX=10 StartY=20.15 StartZ=0 EndX=10 EndY=-20.15 EndZ=0
    g2: LineSegment StartX=10 StartY=-20.15 StartZ=0 EndX=-10 EndY=-20.15 EndZ=0
    g3: LineSegment StartX=-10 StartY=-20.15 StartZ=0 EndX=-10 EndY=20.15 EndZ=0
  constraints (10):
    c: Coincident(g0,g1)
    c: Coincident(g1,g2)
    c: Coincident(g2,g3)
    c: Coincident(g3,g0)
    c: Horizontal(g2)
    c: Vertical(g3)
    c: DistanceX(g0,g0) = 20
    c: DistanceY(g1,g1) = 40.3
    c: Symmetric(g0,g1,g-1)
    c: Symmetric(g0,g0,g-2)
FEATURE [Sketcher::SketchObject] Sketch380
  MapMode = 5
  Placement = pos=(0,0,0) rot=(1,0,0;1.5708rad)
  Support = -> [XZ_Plane109]
  sketch-geometry (1):
    g0: Circle CenterX=0 CenterY=4 CenterZ=0 NormalX=0 NormalY=0 NormalZ=1 AngleXU=0 Radius=0.75
  constraints (3):
    c: PointOnObject(g0,g-2)
    c: Radius(g0) = 0.75
    c: DistanceY(g-1,g0) = 4
FEATURE [Sketcher::SketchObject] Sketch381
  MapMode = 5
  Placement = pos=(0,0,0) rot=(1,0,0;1.5708rad)
  Support = -> [XZ_Plane110]
  sketch-geometry (1):
    g0: Circle CenterX=-1.55 CenterY=4 CenterZ=0 NormalX=0 NormalY=0 NormalZ=1 AngleXU=0 Radius=0.75
  constraints (3):
    c: Radius(g0) = 0.75
    c: DistanceY(g-1,g0) = 4
    c: DistanceX(g0,g-1) = 1.55
FEATURE [Sketcher::SketchObject] Sketch383
  MapMode = 5
  Support = -> [XY_Plane111]
  sketch-geometry (1):
    g0: Circle CenterX=0 CenterY=10.15 CenterZ=0 NormalX=0 NormalY=0 NormalZ=1 AngleXU=0 Radius=3
  constraints (3):
    c: PointOnObject(g0,g-2)
    c: DistanceY(g-1,g0) = 10.15
    c: Radius(g0) = 3
FEATURE [PartDesign::Pad] Pad128  label="Baseblock003"
  Length = 26.6
  Length2 = 100
  Profile = -> Sketch379
  Type = 0
FEATURE [Sketcher::SketchObject] Sketch370
  MapMode = 5
  Placement = pos=(0,0,26.6) rot=(0,0,1;0rad)
  Support = -> [Pad128]
  sketch-geometry (4):
    g0: LineSegment StartX=-10 StartY=-26.8 StartZ=0 EndX=10 EndY=-26.8 EndZ=0
    g1: LineSegment StartX=10 StartY=-26.8 StartZ=0 EndX=10 EndY=26.8 EndZ=0
    g2: LineSegment StartX=10 StartY=26.8 StartZ=0 EndX=-10 EndY=26.8 EndZ=0
    g3: LineSegment StartX=-10 StartY=26.8 StartZ=0 EndX=-10 EndY=-26.8 EndZ=0
  constraints (10):
    c: Coincident(g0,g1)
    c: Coincident(g1,g2)
    c: Coincident(g2,g3)
    c: Coincident(g3,g0)
    c: Horizontal(g0)
    c: Vertical(g3)
    c: Symmetric(g1,g2,g-2)
    c: Symmetric(g1,g0,g-1)
    c: DistanceX(g2,g2) = 20
    c: DistanceY(g1,g1) = 53.6
FEATURE [PartDesign::Pad] Pad130
  Length = 10
  Length2 = 100
  Placement = pos=(0,0,0) rot=(1,0,0;1.5708rad)
  Profile = -> Sketch377
  Reversed = true
  Type = 0
FEATURE [PartDesign::Body] Body074  label="brown wire003"
  Group = -> [Sketch377,Pad130]
  Origin = -> Origin108
  Placement = pos=(0,25.15,0) rot=(0,0,1;0rad)
  Tip = -> Pad130
FEATURE [PartDesign::Pad] Pad131
  Length = 10
  Length2 = 100
  Placement = pos=(0,0,0) rot=(1,0,0;1.5708rad)
  Profile = -> Sketch380
  Reversed = true
  Type = 0
FEATURE [PartDesign::Body] Body077  label="red wire003"
  Group = -> [Sketch380,Pad131]
  Origin = -> Origin112
  Placement = pos=(0,25.15,0) rot=(0,0,1;0rad)
  Tip = -> Pad131
FEATURE [PartDesign::Pad] Pad134
  Length = 5
  Length2 = 100
  Profile = -> Sketch383
  Type = 0
FEATURE [Sketcher::SketchObject] Sketch376
  ExternalGeometry = -> [Pad134]
  MapMode = 5
  Placement = pos=(0,0,5) rot=(0,0,1;0rad)
  Support = -> [Pad134]
  sketch-geometry (1):
    g0: Circle CenterX=0 CenterY=10.15 CenterZ=0 NormalX=0 NormalY=0 NormalZ=1 AngleXU=0 Radius=1.5
  constraints (2):
    c: Coincident(g0,g-3)
    c: Radius(g0) = 1.5
FEATURE [PartDesign::Pad] Pad135
  Length = 10
  Length2 = 100
  Placement = pos=(0,0,0) rot=(1,0,0;1.5708rad)
  Profile = -> Sketch381
  Reversed = true
  Type = 0
FEATURE [PartDesign::Body] Body076  label="orange wire003"
  Group = -> [Sketch381,Pad135]
  Origin = -> Origin107
  Placement = pos=(0,25.15,0) rot=(0,0,1;0rad)
  Tip = -> Pad135
FEATURE [PartDesign::Pad] Pad140
  BaseFeature = -> Pad128
  Length = 2.5
  Length2 = 100
  Profile = -> Sketch370
  Type = 0
FEATURE [Sketcher::SketchObject] Sketch365
  MapMode = 5
  Placement = pos=(0,0,29.1) rot=(0,0,1;0rad)
  Support = -> [Pad140]
  sketch-geometry (4):
    g0: LineSegment StartX=-10 StartY=-20.15 StartZ=0 EndX=10 EndY=-20.15 EndZ=0
    g1: LineSegment StartX=10 StartY=-20.15 StartZ=0 EndX=10 EndY=20.15 EndZ=0
    g2: LineSegment StartX=10 StartY=20.15 StartZ=0 EndX=-10 EndY=20.15 EndZ=0
    g3: LineSegment StartX=-10 StartY=20.15 StartZ=0 EndX=-10 EndY=-20.15 EndZ=0
  constraints (10):
    c: Coincident(g0,g1)
    c: Coincident(g1,g2)
    c: Coincident(g2,g3)
    c: Coincident(g3,g0)
    c: Horizontal(g0)
    c: Vertical(g3)
    c: Symmetric(g1,g2,g-2)
    c: Symmetric(g1,g0,g-1)
    c: DistanceX(g2,g2) = 20
    c: DistanceY(g1,g1) = 40.3
FEATURE [PartDesign::Pad] Pad132
  BaseFeature = -> Pad140
  Length = 6
  Length2 = 100
  Profile = -> Sketch365
  Type = 0
FEATURE [Sketcher::SketchObject] Sketch375
  ExternalGeometry = -> [Pad132]
  MapMode = 5
  Placement = pos=(0,0,35.1) rot=(0,0,1;0rad)
  Support = -> [Pad132]
  sketch-geometry (7):
    g0: ArcOfCircle CenterX=-3e-16 CenterY=10.15 CenterZ=0 NormalX=0 NormalY=0 NormalZ=1 AngleXU=0 Radius=9.5 StartAngle=5.9573 EndAngle=9.75066
    g1: LineSegment StartX=-9 StartY=7.10862 StartZ=0 EndX=-9 EndY=-14.15 EndZ=0
    g2: LineSegment StartX=-9 StartY=-14.15 StartZ=0 EndX=-5 EndY=-14.15 EndZ=0
    g3: LineSegment StartX=5 StartY=-14.15 StartZ=0 EndX=9 EndY=-14.15 EndZ=0
    g4: LineSegment StartX=9 StartY=-14.15 StartZ=0 EndX=9 EndY=7.10862 EndZ=0
    g5: ArcOfCircle CenterX=-3e-16 CenterY=-10.4 CenterZ=0 NormalX=0 NormalY=0 NormalZ=1 AngleXU=0 Radius=6.25 StartAngle=3.78509 EndAngle=5.63968
    g6: LineSegment [constr] StartX=0 StartY=-20.15 StartZ=0 EndX=0 EndY=-16.65 EndZ=0
  constraints (22):
    c: Symmetric(g0,g0,g-2)
    c: Coincident(g1,g0)
    c: Vertical(g1)
    c: Coincident(g2,g1)
    c: Horizontal(g2)
    c: Horizontal(g3)
    c: Coincident(g4,g3)
    c: Coincident(g4,g0)
    c: Vertical(g4)
    c: Symmetric(g2,g3,g-2)
    c: Coincident(g5,g2)
    c: Coincident(g5,g3)
    c: DistanceY(g-3,g3) = 6
    c: DistanceY(g0,g-4) = 10
    c: Radius(g0) = 9.5
    c: DistanceX(g0,g0) = 18
    c: PointOnObject(g6,g-3)
    c: PointOnObject(g6,g5)
    c: Vertical(g6)
    c: DistanceY(g6,g6) = 3.5
    c: DistanceX(g2,g3) = 10
    c: PointOnObject(g6,g-2)
FEATURE [PartDesign::Pad] Pad138
  BaseFeature = -> Pad132
  Length = 2.5
  Length2 = 100
  Profile = -> Sketch375
  Type = 0
FEATURE [Sketcher::SketchObject] Sketch367
  ExternalGeometry = -> [Pad138]
  MapMode = 5
  Placement = pos=(0,0,37.6) rot=(0,0,1;0rad)
  Support = -> [Pad138]
  sketch-geometry (1):
    g0: Circle CenterX=-3e-16 CenterY=10.15 CenterZ=0 NormalX=0 NormalY=0 NormalZ=1 AngleXU=0 Radius=6.5
  constraints (2):
    c: Coincident(g0,g-3)
    c: Radius(g0) = 6.5
FEATURE [PartDesign::Pad] Pad126
  BaseFeature = -> Pad138
  Length = 1
  Length2 = 100
  Profile = -> Sketch367
  Type = 0
FEATURE [Sketcher::SketchObject] Sketch369
  ExternalGeometry = -> [Pad126]
  MapMode = 5
  Placement = pos=(0,0,38.6) rot=(0,0,1;0rad)
  Support = -> [Pad126]
  sketch-geometry (1):
    g0: Circle CenterX=0 CenterY=10.15 CenterZ=0 NormalX=0 NormalY=0 NormalZ=1 AngleXU=0 Radius=5.5
  constraints (2):
    c: Coincident(g0,g-3)
    c: Radius(g0) = 5.5
FEATURE [PartDesign::Pad] Pad133
  BaseFeature = -> Pad126
  Length = 0.5
  Length2 = 100
  Profile = -> Sketch369
  Type = 0
FEATURE [Sketcher::SketchObject] Sketch382
  ExternalGeometry = -> [Pad133]
  MapMode = 5
  Placement = pos=(0,0,39.1) rot=(0,0,1;0rad)
  Support = -> [Pad133]
  sketch-geometry (1):
    g0: Circle CenterX=0 CenterY=10.15 CenterZ=0 NormalX=0 NormalY=0 NormalZ=1 AngleXU=0 Radius=3
  constraints (2):
    c: Coincident(g0,g-3)
    c: Radius(g0) = 3
FEATURE [PartDesign::Pad] Pad129
  BaseFeature = -> Pad133
  Length = 4
  Length2 = 100
  Profile = -> Sketch382
  Type = 0
FEATURE [Sketcher::SketchObject] Sketch372
  ExternalGeometry = -> [Pad129]
  MapMode = 5
  Placement = pos=(0,0,43.1) rot=(0,0,1;0rad)
  Support = -> [Pad129]
  sketch-geometry (1):
    g0: Circle CenterX=0 CenterY=10.15 CenterZ=0 NormalX=0 NormalY=0 NormalZ=1 AngleXU=0 Radius=1.5
  constraints (2):
    c: Coincident(g0,g-3)
    c: Radius(g0) = 1.5
FEATURE [PartDesign::Pocket] Pocket172
  BaseFeature = -> Pad129
  Length = 5
  Length2 = 100
  Profile = -> Sketch372
  Type = 0
FEATURE [Sketcher::SketchObject] Sketch366
  MapMode = 5
  Placement = pos=(0,0,29.1) rot=(0,0,1;0rad)
  Support = -> [Pocket172]
  sketch-geometry (4):
    g0: Circle CenterX=-4.91157 CenterY=25.3 CenterZ=0 NormalX=0 NormalY=0 NormalZ=1 AngleXU=0 Radius=2.25
    g1: Circle CenterX=4.91157 CenterY=25.3 CenterZ=0 NormalX=0 NormalY=0 NormalZ=1 AngleXU=0 Radius=2.25
    g2: Circle CenterX=-4.91157 CenterY=-25.3 CenterZ=0 NormalX=0 NormalY=0 NormalZ=1 AngleXU=0 Radius=2.25
    g3: Circle CenterX=4.91157 CenterY=-25.3 CenterZ=0 NormalX=0 NormalY=0 NormalZ=1 AngleXU=0 Radius=2.25
  constraints (8):
    c: Equal(g3,g2)
    c: Equal(g2,g1)
    c: Equal(g1,g0)
    c: Radius(g1) = 2.25
    c: Symmetric(g1,g0,g-2)
    c: Symmetric(g3,g2,g-2)
    c: Symmetric(g3,g1,g-1)
    c: DistanceY(g3,g1) = 50.6
FEATURE [PartDesign::Pocket] Pocket173
  BaseFeature = -> Pocket172
  Length = 5
  Length2 = 100
  Profile = -> Sketch366
  Type = 0
FEATURE [Sketcher::SketchObject] Sketch378
  MapMode = 5
  Placement = pos=(0,0,29.1) rot=(0,0,1;0rad)
  Support = -> [Pocket173]
  sketch-geometry (8):
    g0: LineSegment StartX=-0.5 StartY=26.8 StartZ=0 EndX=0.5 EndY=26.8 EndZ=0
    g1: LineSegment StartX=0.5 StartY=26.8 StartZ=0 EndX=0.5 EndY=20.15 EndZ=0
    g2: LineSegment StartX=0.5 StartY=20.15 StartZ=0 EndX=-0.5 EndY=20.15 EndZ=0
    g3: LineSegment StartX=-0.5 StartY=20.15 StartZ=0 EndX=-0.5 EndY=26.8 EndZ=0
    g4: LineSegment StartX=-0.5 StartY=-20.15 StartZ=0 EndX=0.5 EndY=-20.15 EndZ=0
    g5: LineSegment StartX=0.5 StartY=-20.15 StartZ=0 EndX=0.5 EndY=-26.8 EndZ=0
    g6: LineSegment StartX=0.5 StartY=-26.8 StartZ=0 EndX=-0.5 EndY=-26.8 EndZ=0
    g7: LineSegment StartX=-0.5 StartY=-26.8 StartZ=0 EndX=-0.5 EndY=-20.15 EndZ=0
  constraints (20):
    c: Coincident(g0,g1)
    c: Coincident(g1,g2)
    c: Coincident(g2,g3)
    c: Coincident(g3,g0)
    c: Horizontal(g2)
    c: Vertical(g1)
    c: Vertical(g3)
    c: Coincident(g4,g5)
    c: Coincident(g5,g6)
    c: Coincident(g6,g7)
    c: Coincident(g7,g4)
    c: Horizontal(g6)
    c: Vertical(g7)
    c: Symmetric(g4,g4,g-2)
    c: Symmetric(g0,g0,g-2)
    c: Symmetric(g0,g5,g-1)
    c: DistanceY(g5,g0) = 53.6
    c: DistanceY(g4,g1) = 40.3
    c: DistanceX(g0,g0) = 1
    c: Symmetric(g4,g1,g-1)
FEATURE [PartDesign::Pad] Pad137
  BaseFeature = -> Pocket173
  Length = 2
  Length2 = 100
  Profile = -> Sketch378
  Type = 0
FEATURE [Sketcher::SketchObject] Sketch371
  ExternalGeometry = -> [Pad137]
  MapMode = 5
  Placement = pos=(0.5,0,0) rot=(0.57735,0.57735,0.57735;2.0944rad)
  Support = -> [Pad137]
  sketch-geometry (6):
    g0: LineSegment StartX=-26.8 StartY=29.1 StartZ=0 EndX=-26.8 EndY=31.1 EndZ=0
    g1: LineSegment StartX=-26.8 StartY=31.1 StartZ=0 EndX=-20.15 EndY=31.1 EndZ=0
    g2: LineSegment StartX=-20.15 StartY=31.1 StartZ=0 EndX=-26.8 EndY=29.1 EndZ=0
    g3: LineSegment StartX=20.15 StartY=31.1 StartZ=0 EndX=26.8 EndY=31.1 EndZ=0
    g4: LineSegment StartX=26.8 StartY=31.1 StartZ=0 EndX=26.8 EndY=29.1 EndZ=0
    g5: LineSegment StartX=26.8 StartY=29.1 StartZ=0 EndX=20.15 EndY=31.1 EndZ=0
  constraints (14):
    c: Vertical(g0)
    c: Coincident(g0,g1)
    c: Horizontal(g1)
    c: Coincident(g1,g2)
    c: Coincident(g2,g0)
    c: Coincident(g3,g4)
    c: Coincident(g4,g5)
    c: Coincident(g5,g3)
    c: Symmetric(g0,g4,g-2)
    c: Symmetric(g3,g0,g-2)
    c: Symmetric(g1,g3,g-2)
    c: DistanceX(g0,g3) = 53.6
    c: DistanceY(g4,g4) = 2
    c: Coincident(g3,g-3)
FEATURE [PartDesign::Pocket] Pocket174
  BaseFeature = -> Pad137
  Length = 1
  Length2 = 100
  Profile = -> Sketch371
  Type = 0
FEATURE [PartDesign::Fillet] Fillet060
  Base = -> Pocket174 [Edge26,Edge27,Edge72,Edge63,Edge70,Edge78,Edge51,Edge49,Edge71,Edge50,Edge79,Edge86,Edge30,Edge21,Edge4,Edge29,Edge105,Edge107,Edge109,Edge111,Edge113,Edge114,Edge123]
  BaseFeature = -> Pocket174
  Radius = 0.4
FEATURE [Sketcher::SketchObject] Sketch374
  MapMode = 5
  Placement = pos=(0,20.15,0) rot=(0,0.707107,0.707107;3.14159rad)
  Support = -> [Fillet060]
  sketch-geometry (4):
    g0: LineSegment StartX=-3.25 StartY=2 StartZ=0 EndX=3.25 EndY=2 EndZ=0
    g1: LineSegment StartX=3.25 StartY=2 StartZ=0 EndX=3.25 EndY=6 EndZ=0
    g2: LineSegment StartX=3.25 StartY=6 StartZ=0 EndX=-3.25 EndY=6 EndZ=0
    g3: LineSegment StartX=-3.25 StartY=6 StartZ=0 EndX=-3.25 EndY=2 EndZ=0
  constraints (11):
    c: Coincident(g0,g1)
    c: Coincident(g1,g2)
    c: Coincident(g2,g3)
    c: Coincident(g3,g0)
    c: Horizontal(g0)
    c: Vertical(g1)
    c: Vertical(g3)
    c: DistanceY(g-1,g0) = 2
    c: DistanceY(g1,g1) = 4
    c: Symmetric(g2,g1,g-2)
    c: DistanceX(g2,g2) = 6.5
FEATURE [PartDesign::Pad] Pad127
  BaseFeature = -> Fillet060
  Length = 1
  Length2 = 100
  Profile = -> Sketch374
  Type = 0
FEATURE [Sketcher::SketchObject] Sketch373
  MapMode = 5
  Placement = pos=(0,21.15,0) rot=(0,0.707107,0.707107;3.14159rad)
  Support = -> [Pad127]
  sketch-geometry (4):
    g0: LineSegment StartX=-2.75 StartY=5.5 StartZ=0 EndX=2.75 EndY=5.5 EndZ=0
    g1: LineSegment StartX=2.75 StartY=5.5 StartZ=0 EndX=2.75 EndY=2.5 EndZ=0
    g2: LineSegment StartX=2.75 StartY=2.5 StartZ=0 EndX=-2.75 EndY=2.5 EndZ=0
    g3: LineSegment StartX=-2.75 StartY=2.5 StartZ=0 EndX=-2.75 EndY=5.5 EndZ=0
  constraints (11):
    c: Coincident(g0,g1)
    c: Coincident(g1,g2)
    c: Coincident(g2,g3)
    c: Coincident(g3,g0)
    c: Horizontal(g0)
    c: Vertical(g1)
    c: Vertical(g3)
    c: Symmetric(g1,g2,g-2)
    c: DistanceY(g1,g0) = 3
    c: DistanceY(g-1,g1) = 2.5
    c: DistanceX(g0,g0) = 5.5
FEATURE [PartDesign::Pad] Pad136
  BaseFeature = -> Pad127
  Length = 4
  Length2 = 100
  Profile = -> Sketch373
  Type = 0
FEATURE [Sketcher::SketchObject] Sketch368
  MapMode = 5
  Placement = pos=(0,0,0) rot=(1,0,0;3.14159rad)
  Support = -> [Pad136]
  sketch-geometry (4):
    g0: LineSegment StartX=-10 StartY=-20.15 StartZ=0 EndX=10 EndY=-20.15 EndZ=0
    g1: LineSegment StartX=10 StartY=-20.15 StartZ=0 EndX=10 EndY=20.15 EndZ=0
    g2: LineSegment StartX=10 StartY=20.15 StartZ=0 EndX=-10 EndY=20.15 EndZ=0
    g3: LineSegment StartX=-10 StartY=20.15 StartZ=0 EndX=-10 EndY=-20.15 EndZ=0
  constraints (10):
    c: Coincident(g0,g1)
    c: Coincident(g1,g2)
    c: Coincident(g2,g3)
    c: Coincident(g3,g0)
    c: Horizontal(g0)
    c: Vertical(g1)
    c: Symmetric(g2,g1,g-2)
    c: Symmetric(g0,g2,g-1)
    c: DistanceX(g2,g2) = 20
    c: DistanceY(g1,g1) = 40.3
FEATURE [PartDesign::Pad] Pad139
  BaseFeature = -> Pad136
  Length = 2
  Length2 = 100
  Profile = -> Sketch368
  Type = 0
FEATURE [PartDesign::Chamfer] Chamfer052
  Base = -> Pad139 [Face7]
  BaseFeature = -> Pad139
  Size = 1.5
FEATURE [PartDesign::Fillet] Fillet059
  Base = -> Chamfer052 [Edge1,Edge7,Edge18,Edge4,Face12]
  BaseFeature = -> Chamfer052
  Radius = 0.4
FEATURE [Sketcher::SketchObject] Sketch364
  ExternalGeometry = -> [Fillet059]
  MapMode = 5
  Placement = pos=(0,0,43.1) rot=(0,0,1;0rad)
  Support = -> [Fillet059]
  sketch-geometry (1):
    g0: Circle CenterX=0 CenterY=10.15 CenterZ=0 NormalX=0 NormalY=0 NormalZ=1 AngleXU=0 Radius=3
  constraints (2):
    c: Coincident(g0,g-3)
    c: Radius(g0) = 3
FEATURE [PartDesign::Pocket] Pocket171
  BaseFeature = -> Fillet059
  Length = 5
  Length2 = 100
  Profile = -> Sketch364
  Type = 0
FEATURE [PartDesign::Body] Body075  label="MG996R002"
  Group = -> [Sketch379,Pad128,Sketch370,Pad140,Sketch365,Pad132,Sketch375,Pad138,Sketch367,Pad126,Sketch369,Pad133,Sketch382,Pad129,Sketch372,Pocket172,Sketch366,Pocket173,Sketch378,Pad137,Sketch371,Pocket174,Fillet060,Sketch374,Pad127,Sketch373,Pad136,Sketch368,Pad139,Chamfer052,Fillet059,Sketch364,Pocket171]
  Origin = -> Origin111
  Tip = -> Pocket171
FEATURE [PartDesign::Pocket] Pocket175
  BaseFeature = -> Pad134
  Length = 4
  Length2 = 100
  Profile = -> Sketch376
  Type = 0
FEATURE [PartDesign::Chamfer] Chamfer053
  Base = -> Pocket175 [Edge3]
  BaseFeature = -> Pocket175
  Size = 0.25
FEATURE [PartDesign::Body] Body073  label="Gear003"
  Group = -> [Sketch383,Pad134,Sketch376,Pocket175,Chamfer053]
  Origin = -> Origin109
  Placement = pos=(0,0,38.25) rot=(0,0,1;0rad)
  Tip = -> Chamfer053
FEATURE [App::Part] Part031  label="Servo002"
  Group = -> [Body075,Body073,Body077,Body076,Body074]
  Origin = -> Origin110
  Placement = pos=(-47.3841,6.65,56.9914) rot=(-0.57735,-0.57735,0.57735;4.18879rad)
FEATURE [Sketcher::SketchObject] Sketch385
  MapMode = 5
  Support = -> [XY_Plane113]
  sketch-geometry (1):
    g0: Circle CenterX=0 CenterY=0 CenterZ=0 NormalX=0 NormalY=0 NormalZ=1 AngleXU=0 Radius=2.75
  constraints (2):
    c: Coincident(g0,g-1)
    c: Radius(g0) = 2.75
FEATURE [PartDesign::Pad] Pad004  label="M3x20 Head004"
  Length = 3
  Length2 = 100
  Profile = -> Sketch385
  Type = 0
FEATURE [Sketcher::SketchObject] Sketch386
  MapMode = 5
  Placement = pos=(0,0,3) rot=(0,0,1;0rad)
  Support = -> [Pad004]
  sketch-geometry (1):
    g0: Circle CenterX=0 CenterY=0 CenterZ=0 NormalX=0 NormalY=0 NormalZ=1 AngleXU=0 Radius=1.5
  constraints (2):
    c: Coincident(g0,g-1)
    c: Radius(g0) = 1.5
FEATURE [PartDesign::Pad] Pad003  label="M3x20 Thread004"
  BaseFeature = -> Pad004
  Length = 20
  Length2 = 100
  Profile = -> Sketch386
  Type = 0
FEATURE [Sketcher::SketchObject] Sketch384
  MapMode = 5
  Placement = pos=(0,0,0) rot=(1,0,0;3.14159rad)
  Support = -> [Pad003]
  sketch-geometry (7):
    g0: LineSegment StartX=1.275 StartY=0.736122 StartZ=0 EndX=0 EndY=1.47224 EndZ=0
    g1: LineSegment StartX=0 StartY=1.47224 StartZ=0 EndX=-1.275 EndY=0.736122 EndZ=0
    g2: LineSegment StartX=-1.275 StartY=0.736122 StartZ=0 EndX=-1.275 EndY=-0.736122 EndZ=0
    g3: LineSegment StartX=-1.275 StartY=-0.736122 StartZ=0 EndX=1.34766e-11 EndY=-1.47224 EndZ=0
    g4: LineSegment StartX=1.34766e-11 StartY=-1.47224 StartZ=0 EndX=1.275 EndY=-0.736122 EndZ=0
    g5: LineSegment StartX=1.275 StartY=-0.736122 StartZ=0 EndX=1.275 EndY=0.736122 EndZ=0
    g6: Circle [constr] CenterX=0 CenterY=0 CenterZ=0 NormalX=0 NormalY=0 NormalZ=1 AngleXU=0 Radius=1.47224
  constraints (16):
    c: Coincident(g0,g1)
    c: Coincident(g1,g2)
    c: Coincident(g2,g3)
    c: Coincident(g3,g4)
    c: Coincident(g4,g5)
    c: Coincident(g5,g0)
    c: Equal(g0, g1-g5) x5
    c: PointOnObject(g0,g6)
    c: PointOnObject(g1,g6)
    c: PointOnObject(g2,g6)
    c: PointOnObject(g3,g6)
    c: PointOnObject(g4,g6)
    c: PointOnObject(g5,g6)
    c: Coincident(g6,g-1)
    c: PointOnObject(g0,g-2)
    c: DistanceX(g1,g0) = 2.55
FEATURE [PartDesign::Pocket] Pocket176  label="M3x20 Wrench004"
  BaseFeature = -> Pad003
  Length = 1.3
  Length2 = 100
  Profile = -> Sketch384
  Type = 0
FEATURE [PartDesign::Chamfer] Chamfer054  label="M3x20 Smooth004"
  Base = -> Pocket176 [Face11,Edge2,Edge24,Edge3]
  BaseFeature = -> Pocket176
  Size = 0.2
FEATURE [PartDesign::Body] Body078  label="M3x013"
  Group = -> [Sketch385,Pad004,Sketch386,Pad003,Sketch384,Pocket176,Chamfer054]
  Origin = -> Origin113
  Placement = pos=(-115.35,-29.35,62.05) rot=(-1,0,0;1.5708rad)
  Tip = -> Chamfer054
FEATURE [Sketcher::SketchObject] Sketch388
  MapMode = 5
  Support = -> [XY_Plane114]
  sketch-geometry (1):
    g0: Circle CenterX=0 CenterY=0 CenterZ=0 NormalX=0 NormalY=0 NormalZ=1 AngleXU=0 Radius=2.75
  constraints (2):
    c: Coincident(g0,g-1)
    c: Radius(g0) = 2.75
FEATURE [PartDesign::Pad] Pad142  label="M3x20 Head005"
  Length = 3
  Length2 = 100
  Profile = -> Sketch388
  Type = 0
FEATURE [Sketcher::SketchObject] Sketch389
  MapMode = 5
  Placement = pos=(0,0,3) rot=(0,0,1;0rad)
  Support = -> [Pad142]
  sketch-geometry (1):
    g0: Circle CenterX=0 CenterY=0 CenterZ=0 NormalX=0 NormalY=0 NormalZ=1 AngleXU=0 Radius=1.5
  constraints (2):
    c: Coincident(g0,g-1)
    c: Radius(g0) = 1.5
FEATURE [PartDesign::Pad] Pad141  label="M3x20 Thread005"
  BaseFeature = -> Pad142
  Length = 20
  Length2 = 100
  Profile = -> Sketch389
  Type = 0
FEATURE [Sketcher::SketchObject] Sketch387
  MapMode = 5
  Placement = pos=(0,0,0) rot=(1,0,0;3.14159rad)
  Support = -> [Pad141]
  sketch-geometry (7):
    g0: LineSegment StartX=1.275 StartY=0.736122 StartZ=0 EndX=0 EndY=1.47224 EndZ=0
    g1: LineSegment StartX=0 StartY=1.47224 StartZ=0 EndX=-1.275 EndY=0.736122 EndZ=0
    g2: LineSegment StartX=-1.275 StartY=0.736122 StartZ=0 EndX=-1.275 EndY=-0.736122 EndZ=0
    g3: LineSegment StartX=-1.275 StartY=-0.736122 StartZ=0 EndX=1.34766e-11 EndY=-1.47224 EndZ=0
    g4: LineSegment StartX=1.34766e-11 StartY=-1.47224 StartZ=0 EndX=1.275 EndY=-0.736122 EndZ=0
    g5: LineSegment StartX=1.275 StartY=-0.736122 StartZ=0 EndX=1.275 EndY=0.736122 EndZ=0
    g6: Circle [constr] CenterX=0 CenterY=0 CenterZ=0 NormalX=0 NormalY=0 NormalZ=1 AngleXU=0 Radius=1.47224
  constraints (16):
    c: Coincident(g0,g1)
    c: Coincident(g1,g2)
    c: Coincident(g2,g3)
    c: Coincident(g3,g4)
    c: Coincident(g4,g5)
    c: Coincident(g5,g0)
    c: Equal(g0, g1-g5) x5
    c: PointOnObject(g0,g6)
    c: PointOnObject(g1,g6)
    c: PointOnObject(g2,g6)
    c: PointOnObject(g3,g6)
    c: PointOnObject(g4,g6)
    c: PointOnObject(g5,g6)
    c: Coincident(g6,g-1)
    c: PointOnObject(g0,g-2)
    c: DistanceX(g1,g0) = 2.55
FEATURE [PartDesign::Pocket] Pocket177  label="M3x20 Wrench005"
  BaseFeature = -> Pad141
  Length = 1.3
  Length2 = 100
  Profile = -> Sketch387
  Type = 0
FEATURE [PartDesign::Chamfer] Chamfer055  label="M3x20 Smooth005"
  Base = -> Pocket177 [Face11,Edge2,Edge24,Edge3]
  BaseFeature = -> Pocket177
  Size = 0.2
FEATURE [PartDesign::Body] Body079  label="M3x014"
  Group = -> [Sketch388,Pad142,Sketch389,Pad141,Sketch387,Pocket177,Chamfer055]
  Origin = -> Origin114
  Placement = pos=(-110.55,-29.35,52.05) rot=(-1,0,0;1.5708rad)
  Tip = -> Chamfer055
FEATURE [Sketcher::SketchObject] Sketch391
  MapMode = 5
  Support = -> [XY_Plane115]
  sketch-geometry (1):
    g0: Circle CenterX=0 CenterY=0 CenterZ=0 NormalX=0 NormalY=0 NormalZ=1 AngleXU=0 Radius=2.75
  constraints (2):
    c: Coincident(g0,g-1)
    c: Radius(g0) = 2.75
FEATURE [PartDesign::Pad] Pad144  label="M3x20 Head006"
  Length = 3
  Length2 = 100
  Profile = -> Sketch391
  Type = 0
FEATURE [Sketcher::SketchObject] Sketch392
  MapMode = 5
  Placement = pos=(0,0,3) rot=(0,0,1;0rad)
  Support = -> [Pad144]
  sketch-geometry (1):
    g0: Circle CenterX=0 CenterY=0 CenterZ=0 NormalX=0 NormalY=0 NormalZ=1 AngleXU=0 Radius=1.5
  constraints (2):
    c: Coincident(g0,g-1)
    c: Radius(g0) = 1.5
FEATURE [PartDesign::Pad] Pad143  label="M3x20 Thread006"
  BaseFeature = -> Pad144
  Length = 20
  Length2 = 100
  Profile = -> Sketch392
  Type = 0
FEATURE [Sketcher::SketchObject] Sketch390
  MapMode = 5
  Placement = pos=(0,0,0) rot=(1,0,0;3.14159rad)
  Support = -> [Pad143]
  sketch-geometry (7):
    g0: LineSegment StartX=1.275 StartY=0.736122 StartZ=0 EndX=0 EndY=1.47224 EndZ=0
    g1: LineSegment StartX=0 StartY=1.47224 StartZ=0 EndX=-1.275 EndY=0.736122 EndZ=0
    g2: LineSegment StartX=-1.275 StartY=0.736122 StartZ=0 EndX=-1.275 EndY=-0.736122 EndZ=0
    g3: LineSegment StartX=-1.275 StartY=-0.736122 StartZ=0 EndX=1.34766e-11 EndY=-1.47224 EndZ=0
    g4: LineSegment StartX=1.34766e-11 StartY=-1.47224 StartZ=0 EndX=1.275 EndY=-0.736122 EndZ=0
    g5: LineSegment StartX=1.275 StartY=-0.736122 StartZ=0 EndX=1.275 EndY=0.736122 EndZ=0
    g6: Circle [constr] CenterX=0 CenterY=0 CenterZ=0 NormalX=0 NormalY=0 NormalZ=1 AngleXU=0 Radius=1.47224
  constraints (16):
    c: Coincident(g0,g1)
    c: Coincident(g1,g2)
    c: Coincident(g2,g3)
    c: Coincident(g3,g4)
    c: Coincident(g4,g5)
    c: Coincident(g5,g0)
    c: Equal(g0, g1-g5) x5
    c: PointOnObject(g0,g6)
    c: PointOnObject(g1,g6)
    c: PointOnObject(g2,g6)
    c: PointOnObject(g3,g6)
    c: PointOnObject(g4,g6)
    c: PointOnObject(g5,g6)
    c: Coincident(g6,g-1)
    c: PointOnObject(g0,g-2)
    c: DistanceX(g1,g0) = 2.55
FEATURE [PartDesign::Pocket] Pocket178  label="M3x20 Wrench006"
  BaseFeature = -> Pad143
  Length = 1.3
  Length2 = 100
  Profile = -> Sketch390
  Type = 0
FEATURE [PartDesign::Chamfer] Chamfer056  label="M3x20 Smooth006"
  Base = -> Pocket178 [Face11,Edge2,Edge24,Edge3]
  BaseFeature = -> Pocket178
  Size = 0.2
FEATURE [PartDesign::Body] Body080  label="M3x015"
  Group = -> [Sketch391,Pad144,Sketch392,Pad143,Sketch390,Pocket178,Chamfer056]
  Origin = -> Origin115
  Placement = pos=(-71.5,-25.55,62.05) rot=(-1,0,0;1.5708rad)
  Tip = -> Chamfer056
FEATURE [Sketcher::SketchObject] Sketch394
  MapMode = 5
  Support = -> [XY_Plane116]
  sketch-geometry (1):
    g0: Circle CenterX=0 CenterY=0 CenterZ=0 NormalX=0 NormalY=0 NormalZ=1 AngleXU=0 Radius=2.75
  constraints (2):
    c: Coincident(g0,g-1)
    c: Radius(g0) = 2.75
FEATURE [PartDesign::Pad] Pad146  label="M3x20 Head007"
  Length = 3
  Length2 = 100
  Profile = -> Sketch394
  Type = 0
FEATURE [Sketcher::SketchObject] Sketch395
  MapMode = 5
  Placement = pos=(0,0,3) rot=(0,0,1;0rad)
  Support = -> [Pad146]
  sketch-geometry (1):
    g0: Circle CenterX=0 CenterY=0 CenterZ=0 NormalX=0 NormalY=0 NormalZ=1 AngleXU=0 Radius=1.5
  constraints (2):
    c: Coincident(g0,g-1)
    c: Radius(g0) = 1.5
FEATURE [PartDesign::Pad] Pad145  label="M3x20 Thread007"
  BaseFeature = -> Pad146
  Length = 20
  Length2 = 100
  Profile = -> Sketch395
  Type = 0
FEATURE [Sketcher::SketchObject] Sketch393
  MapMode = 5
  Placement = pos=(0,0,0) rot=(1,0,0;3.14159rad)
  Support = -> [Pad145]
  sketch-geometry (7):
    g0: LineSegment StartX=1.275 StartY=0.736122 StartZ=0 EndX=0 EndY=1.47224 EndZ=0
    g1: LineSegment StartX=0 StartY=1.47224 StartZ=0 EndX=-1.275 EndY=0.736122 EndZ=0
    g2: LineSegment StartX=-1.275 StartY=0.736122 StartZ=0 EndX=-1.275 EndY=-0.736122 EndZ=0
    g3: LineSegment StartX=-1.275 StartY=-0.736122 StartZ=0 EndX=1.34766e-11 EndY=-1.47224 EndZ=0
    g4: LineSegment StartX=1.34766e-11 StartY=-1.47224 StartZ=0 EndX=1.275 EndY=-0.736122 EndZ=0
    g5: LineSegment StartX=1.275 StartY=-0.736122 StartZ=0 EndX=1.275 EndY=0.736122 EndZ=0
    g6: Circle [constr] CenterX=0 CenterY=0 CenterZ=0 NormalX=0 NormalY=0 NormalZ=1 AngleXU=0 Radius=1.47224
  constraints (16):
    c: Coincident(g0,g1)
    c: Coincident(g1,g2)
    c: Coincident(g2,g3)
    c: Coincident(g3,g4)
    c: Coincident(g4,g5)
    c: Coincident(g5,g0)
    c: Equal(g0, g1-g5) x5
    c: PointOnObject(g0,g6)
    c: PointOnObject(g1,g6)
    c: PointOnObject(g2,g6)
    c: PointOnObject(g3,g6)
    c: PointOnObject(g4,g6)
    c: PointOnObject(g5,g6)
    c: Coincident(g6,g-1)
    c: PointOnObject(g0,g-2)
    c: DistanceX(g1,g0) = 2.55
FEATURE [PartDesign::Pocket] Pocket179  label="M3x20 Wrench007"
  BaseFeature = -> Pad145
  Length = 1.3
  Length2 = 100
  Profile = -> Sketch393
  Type = 0
FEATURE [PartDesign::Chamfer] Chamfer057  label="M3x20 Smooth007"
  Base = -> Pocket179 [Face11,Edge2,Edge24,Edge3]
  BaseFeature = -> Pocket179
  Size = 0.2
FEATURE [PartDesign::Body] Body081  label="M3x016"
  Group = -> [Sketch394,Pad146,Sketch395,Pad145,Sketch393,Pocket179,Chamfer057]
  Origin = -> Origin116
  Placement = pos=(-71.6,-25.55,52.05) rot=(-1,0,0;1.5708rad)
  Tip = -> Chamfer057
FEATURE [Sketcher::SketchObject] Sketch397
  MapMode = 5
  Support = -> [XY_Plane117]
  sketch-geometry (1):
    g0: Circle CenterX=0 CenterY=0 CenterZ=0 NormalX=0 NormalY=0 NormalZ=1 AngleXU=0 Radius=2.75
  constraints (2):
    c: Coincident(g0,g-1)
    c: Radius(g0) = 2.75
FEATURE [PartDesign::Pad] Pad148  label="M3x20 Head008"
  Length = 3
  Length2 = 100
  Profile = -> Sketch397
  Type = 0
FEATURE [Sketcher::SketchObject] Sketch398
  MapMode = 5
  Placement = pos=(0,0,3) rot=(0,0,1;0rad)
  Support = -> [Pad148]
  sketch-geometry (1):
    g0: Circle CenterX=0 CenterY=0 CenterZ=0 NormalX=0 NormalY=0 NormalZ=1 AngleXU=0 Radius=1.5
  constraints (2):
    c: Coincident(g0,g-1)
    c: Radius(g0) = 1.5
FEATURE [PartDesign::Pad] Pad147  label="M3x20 Thread008"
  BaseFeature = -> Pad148
  Length = 20
  Length2 = 100
  Profile = -> Sketch398
  Type = 0
FEATURE [Sketcher::SketchObject] Sketch396
  MapMode = 5
  Placement = pos=(0,0,0) rot=(1,0,0;3.14159rad)
  Support = -> [Pad147]
  sketch-geometry (7):
    g0: LineSegment StartX=1.275 StartY=0.736122 StartZ=0 EndX=0 EndY=1.47224 EndZ=0
    g1: LineSegment StartX=0 StartY=1.47224 StartZ=0 EndX=-1.275 EndY=0.736122 EndZ=0
    g2: LineSegment StartX=-1.275 StartY=0.736122 StartZ=0 EndX=-1.275 EndY=-0.736122 EndZ=0
    g3: LineSegment StartX=-1.275 StartY=-0.736122 StartZ=0 EndX=1.34766e-11 EndY=-1.47224 EndZ=0
    g4: LineSegment StartX=1.34766e-11 StartY=-1.47224 StartZ=0 EndX=1.275 EndY=-0.736122 EndZ=0
    g5: LineSegment StartX=1.275 StartY=-0.736122 StartZ=0 EndX=1.275 EndY=0.736122 EndZ=0
    g6: Circle [constr] CenterX=0 CenterY=0 CenterZ=0 NormalX=0 NormalY=0 NormalZ=1 AngleXU=0 Radius=1.47224
  constraints (16):
    c: Coincident(g0,g1)
    c: Coincident(g1,g2)
    c: Coincident(g2,g3)
    c: Coincident(g3,g4)
    c: Coincident(g4,g5)
    c: Coincident(g5,g0)
    c: Equal(g0, g1-g5) x5
    c: PointOnObject(g0,g6)
    c: PointOnObject(g1,g6)
    c: PointOnObject(g2,g6)
    c: PointOnObject(g3,g6)
    c: PointOnObject(g4,g6)
    c: PointOnObject(g5,g6)
    c: Coincident(g6,g-1)
    c: PointOnObject(g0,g-2)
    c: DistanceX(g1,g0) = 2.55
FEATURE [PartDesign::Pocket] Pocket180  label="M3x20 Wrench008"
  BaseFeature = -> Pad147
  Length = 1.3
  Length2 = 100
  Profile = -> Sketch396
  Type = 0
FEATURE [PartDesign::Chamfer] Chamfer058  label="M3x20 Smooth008"
  Base = -> Pocket180 [Face11,Edge2,Edge24,Edge3]
  BaseFeature = -> Pocket180
  Size = 0.2
FEATURE [PartDesign::Body] Body082  label="M3x017"
  Group = -> [Sketch397,Pad148,Sketch398,Pad147,Sketch396,Pocket180,Chamfer058]
  Origin = -> Origin117
  Placement = pos=(-23,-25.6,62.05) rot=(-1,0,0;1.5708rad)
  Tip = -> Chamfer058
FEATURE [Sketcher::SketchObject] Sketch400
  MapMode = 5
  Support = -> [XY_Plane118]
  sketch-geometry (1):
    g0: Circle CenterX=0 CenterY=0 CenterZ=0 NormalX=0 NormalY=0 NormalZ=1 AngleXU=0 Radius=2.75
  constraints (2):
    c: Coincident(g0,g-1)
    c: Radius(g0) = 2.75
FEATURE [PartDesign::Pad] Pad150  label="M3x20 Head009"
  Length = 3
  Length2 = 100
  Profile = -> Sketch400
  Type = 0
FEATURE [Sketcher::SketchObject] Sketch401
  MapMode = 5
  Placement = pos=(0,0,3) rot=(0,0,1;0rad)
  Support = -> [Pad150]
  sketch-geometry (1):
    g0: Circle CenterX=0 CenterY=0 CenterZ=0 NormalX=0 NormalY=0 NormalZ=1 AngleXU=0 Radius=1.5
  constraints (2):
    c: Coincident(g0,g-1)
    c: Radius(g0) = 1.5
FEATURE [PartDesign::Pad] Pad149  label="M3x20 Thread009"
  BaseFeature = -> Pad150
  Length = 20
  Length2 = 100
  Profile = -> Sketch401
  Type = 0
FEATURE [Sketcher::SketchObject] Sketch399
  MapMode = 5
  Placement = pos=(0,0,0) rot=(1,0,0;3.14159rad)
  Support = -> [Pad149]
  sketch-geometry (7):
    g0: LineSegment StartX=1.275 StartY=0.736122 StartZ=0 EndX=0 EndY=1.47224 EndZ=0
    g1: LineSegment StartX=0 StartY=1.47224 StartZ=0 EndX=-1.275 EndY=0.736122 EndZ=0
    g2: LineSegment StartX=-1.275 StartY=0.736122 StartZ=0 EndX=-1.275 EndY=-0.736122 EndZ=0
    g3: LineSegment StartX=-1.275 StartY=-0.736122 StartZ=0 EndX=1.34766e-11 EndY=-1.47224 EndZ=0
    g4: LineSegment StartX=1.34766e-11 StartY=-1.47224 StartZ=0 EndX=1.275 EndY=-0.736122 EndZ=0
    g5: LineSegment StartX=1.275 StartY=-0.736122 StartZ=0 EndX=1.275 EndY=0.736122 EndZ=0
    g6: Circle [constr] CenterX=0 CenterY=0 CenterZ=0 NormalX=0 NormalY=0 NormalZ=1 AngleXU=0 Radius=1.47224
  constraints (16):
    c: Coincident(g0,g1)
    c: Coincident(g1,g2)
    c: Coincident(g2,g3)
    c: Coincident(g3,g4)
    c: Coincident(g4,g5)
    c: Coincident(g5,g0)
    c: Equal(g0, g1-g5) x5
    c: PointOnObject(g0,g6)
    c: PointOnObject(g1,g6)
    c: PointOnObject(g2,g6)
    c: PointOnObject(g3,g6)
    c: PointOnObject(g4,g6)
    c: PointOnObject(g5,g6)
    c: Coincident(g6,g-1)
    c: PointOnObject(g0,g-2)
    c: DistanceX(g1,g0) = 2.55
FEATURE [PartDesign::Pocket] Pocket181  label="M3x20 Wrench009"
  BaseFeature = -> Pad149
  Length = 1.3
  Length2 = 100
  Profile = -> Sketch399
  Type = 0
FEATURE [PartDesign::Chamfer] Chamfer059  label="M3x20 Smooth009"
  Base = -> Pocket181 [Face11,Edge2,Edge24,Edge3]
  BaseFeature = -> Pocket181
  Size = 0.2
FEATURE [PartDesign::Body] Body083  label="M3x018"
  Group = -> [Sketch400,Pad150,Sketch401,Pad149,Sketch399,Pocket181,Chamfer059]
  Origin = -> Origin118
  Placement = pos=(-23.1,-25.6,52) rot=(-1,0,0;1.5708rad)
  Tip = -> Chamfer059
FEATURE [Sketcher::SketchObject] Sketch403
  MapMode = 5
  Support = -> [XY_Plane119]
  sketch-geometry (1):
    g0: Circle CenterX=0 CenterY=0 CenterZ=0 NormalX=0 NormalY=0 NormalZ=1 AngleXU=0 Radius=2.75
  constraints (2):
    c: Coincident(g0,g-1)
    c: Radius(g0) = 2.75
FEATURE [PartDesign::Pad] Pad152  label="M3x20 Head010"
  Length = 3
  Length2 = 100
  Profile = -> Sketch403
  Type = 0
FEATURE [Sketcher::SketchObject] Sketch404
  MapMode = 5
  Placement = pos=(0,0,3) rot=(0,0,1;0rad)
  Support = -> [Pad152]
  sketch-geometry (1):
    g0: Circle CenterX=0 CenterY=0 CenterZ=0 NormalX=0 NormalY=0 NormalZ=1 AngleXU=0 Radius=1.5
  constraints (2):
    c: Coincident(g0,g-1)
    c: Radius(g0) = 1.5
FEATURE [PartDesign::Pad] Pad151  label="M3x20 Thread010"
  BaseFeature = -> Pad152
  Length = 20
  Length2 = 100
  Profile = -> Sketch404
  Type = 0
FEATURE [Sketcher::SketchObject] Sketch402
  MapMode = 5
  Placement = pos=(0,0,0) rot=(1,0,0;3.14159rad)
  Support = -> [Pad151]
  sketch-geometry (7):
    g0: LineSegment StartX=1.275 StartY=0.736122 StartZ=0 EndX=0 EndY=1.47224 EndZ=0
    g1: LineSegment StartX=0 StartY=1.47224 StartZ=0 EndX=-1.275 EndY=0.736122 EndZ=0
    g2: LineSegment StartX=-1.275 StartY=0.736122 StartZ=0 EndX=-1.275 EndY=-0.736122 EndZ=0
    g3: LineSegment StartX=-1.275 StartY=-0.736122 StartZ=0 EndX=1.34766e-11 EndY=-1.47224 EndZ=0
    g4: LineSegment StartX=1.34766e-11 StartY=-1.47224 StartZ=0 EndX=1.275 EndY=-0.736122 EndZ=0
    g5: LineSegment StartX=1.275 StartY=-0.736122 StartZ=0 EndX=1.275 EndY=0.736122 EndZ=0
    g6: Circle [constr] CenterX=0 CenterY=0 CenterZ=0 NormalX=0 NormalY=0 NormalZ=1 AngleXU=0 Radius=1.47224
  constraints (16):
    c: Coincident(g0,g1)
    c: Coincident(g1,g2)
    c: Coincident(g2,g3)
    c: Coincident(g3,g4)
    c: Coincident(g4,g5)
    c: Coincident(g5,g0)
    c: Equal(g0, g1-g5) x5
    c: PointOnObject(g0,g6)
    c: PointOnObject(g1,g6)
    c: PointOnObject(g2,g6)
    c: PointOnObject(g3,g6)
    c: PointOnObject(g4,g6)
    c: PointOnObject(g5,g6)
    c: Coincident(g6,g-1)
    c: PointOnObject(g0,g-2)
    c: DistanceX(g1,g0) = 2.55
FEATURE [PartDesign::Pocket] Pocket182  label="M3x20 Wrench010"
  BaseFeature = -> Pad151
  Length = 1.3
  Length2 = 100
  Profile = -> Sketch402
  Type = 0
FEATURE [PartDesign::Chamfer] Chamfer060  label="M3x20 Smooth010"
  Base = -> Pocket182 [Face11,Edge2,Edge24,Edge3]
  BaseFeature = -> Pocket182
  Size = 0.2
FEATURE [PartDesign::Body] Body084  label="M3x019"
  Group = -> [Sketch403,Pad152,Sketch404,Pad151,Sketch402,Pocket182,Chamfer060]
  Origin = -> Origin119
  Placement = pos=(-115.35,28,62.05) rot=(1,0,0;1.5708rad)
  Tip = -> Chamfer060
FEATURE [Sketcher::SketchObject] Sketch406
  MapMode = 5
  Support = -> [XY_Plane120]
  sketch-geometry (1):
    g0: Circle CenterX=0 CenterY=0 CenterZ=0 NormalX=0 NormalY=0 NormalZ=1 AngleXU=0 Radius=2.75
  constraints (2):
    c: Coincident(g0,g-1)
    c: Radius(g0) = 2.75
FEATURE [PartDesign::Pad] Pad154  label="M3x20 Head011"
  Length = 3
  Length2 = 100
  Profile = -> Sketch406
  Type = 0
FEATURE [Sketcher::SketchObject] Sketch407
  MapMode = 5
  Placement = pos=(0,0,3) rot=(0,0,1;0rad)
  Support = -> [Pad154]
  sketch-geometry (1):
    g0: Circle CenterX=0 CenterY=0 CenterZ=0 NormalX=0 NormalY=0 NormalZ=1 AngleXU=0 Radius=1.5
  constraints (2):
    c: Coincident(g0,g-1)
    c: Radius(g0) = 1.5
FEATURE [PartDesign::Pad] Pad153  label="M3x20 Thread011"
  BaseFeature = -> Pad154
  Length = 20
  Length2 = 100
  Profile = -> Sketch407
  Type = 0
FEATURE [Sketcher::SketchObject] Sketch405
  MapMode = 5
  Placement = pos=(0,0,0) rot=(1,0,0;3.14159rad)
  Support = -> [Pad153]
  sketch-geometry (7):
    g0: LineSegment StartX=1.275 StartY=0.736122 StartZ=0 EndX=0 EndY=1.47224 EndZ=0
    g1: LineSegment StartX=0 StartY=1.47224 StartZ=0 EndX=-1.275 EndY=0.736122 EndZ=0
    g2: LineSegment StartX=-1.275 StartY=0.736122 StartZ=0 EndX=-1.275 EndY=-0.736122 EndZ=0
    g3: LineSegment StartX=-1.275 StartY=-0.736122 StartZ=0 EndX=1.34766e-11 EndY=-1.47224 EndZ=0
    g4: LineSegment StartX=1.34766e-11 StartY=-1.47224 StartZ=0 EndX=1.275 EndY=-0.736122 EndZ=0
    g5: LineSegment StartX=1.275 StartY=-0.736122 StartZ=0 EndX=1.275 EndY=0.736122 EndZ=0
    g6: Circle [constr] CenterX=0 CenterY=0 CenterZ=0 NormalX=0 NormalY=0 NormalZ=1 AngleXU=0 Radius=1.47224
  constraints (16):
    c: Coincident(g0,g1)
    c: Coincident(g1,g2)
    c: Coincident(g2,g3)
    c: Coincident(g3,g4)
    c: Coincident(g4,g5)
    c: Coincident(g5,g0)
    c: Equal(g0, g1-g5) x5
    c: PointOnObject(g0,g6)
    c: PointOnObject(g1,g6)
    c: PointOnObject(g2,g6)
    c: PointOnObject(g3,g6)
    c: PointOnObject(g4,g6)
    c: PointOnObject(g5,g6)
    c: Coincident(g6,g-1)
    c: PointOnObject(g0,g-2)
    c: DistanceX(g1,g0) = 2.55
FEATURE [PartDesign::Pocket] Pocket183  label="M3x20 Wrench011"
  BaseFeature = -> Pad153
  Length = 1.3
  Length2 = 100
  Profile = -> Sketch405
  Type = 0
FEATURE [PartDesign::Chamfer] Chamfer061  label="M3x20 Smooth011"
  Base = -> Pocket183 [Face11,Edge2,Edge24,Edge3]
  BaseFeature = -> Pocket183
  Size = 0.2
FEATURE [PartDesign::Body] Body085  label="M3x020"
  Group = -> [Sketch406,Pad154,Sketch407,Pad153,Sketch405,Pocket183,Chamfer061]
  Origin = -> Origin120
  Placement = pos=(-110.55,28,52.05) rot=(1,0,0;1.5708rad)
  Tip = -> Chamfer061
FEATURE [App::Part] Part032  label="Shell Screws"
  Group = -> [Body078,Body079,Body084,Body085]
  Origin = -> Origin121
FEATURE [App::Part] Part033  label="Servo Screws"
  Group = -> [Body080,Body081,Body082,Body083]
  Origin = -> Origin122
FEATURE [Sketcher::SketchObject] Sketch408
  MapMode = 5
  Support = -> [XY_Plane123]
  sketch-geometry (1):
    g0: Circle CenterX=0 CenterY=0 CenterZ=0 NormalX=0 NormalY=0 NormalZ=1 AngleXU=0 Radius=2.75
  constraints (2):
    c: Coincident(g0,g-1)
    c: Radius(g0) = 2.75
FEATURE [PartDesign::Pad] Pad156  label="M3x8 Head015"
  Length = 3
  Length2 = 100
  Profile = -> Sketch408
  Type = 0
FEATURE [Sketcher::SketchObject] Sketch410
  MapMode = 5
  Placement = pos=(0,0,3) rot=(0,0,1;0rad)
  Support = -> [Pad156]
  sketch-geometry (1):
    g0: Circle CenterX=0 CenterY=0 CenterZ=0 NormalX=0 NormalY=0 NormalZ=1 AngleXU=0 Radius=1.5
  constraints (2):
    c: Coincident(g0,g-1)
    c: Radius(g0) = 1.5
FEATURE [PartDesign::Pad] Pad155  label="M3x8 Thread015"
  BaseFeature = -> Pad156
  Length = 8
  Length2 = 100
  Profile = -> Sketch410
  Type = 0
FEATURE [Sketcher::SketchObject] Sketch409
  MapMode = 5
  Placement = pos=(0,0,0) rot=(1,0,0;3.14159rad)
  Support = -> [Pad155]
  sketch-geometry (7):
    g0: LineSegment StartX=1.275 StartY=0.736122 StartZ=0 EndX=0 EndY=1.47224 EndZ=0
    g1: LineSegment StartX=0 StartY=1.47224 StartZ=0 EndX=-1.275 EndY=0.736122 EndZ=0
    g2: LineSegment StartX=-1.275 StartY=0.736122 StartZ=0 EndX=-1.275 EndY=-0.736122 EndZ=0
    g3: LineSegment StartX=-1.275 StartY=-0.736122 StartZ=0 EndX=1.34766e-11 EndY=-1.47224 EndZ=0
    g4: LineSegment StartX=1.34766e-11 StartY=-1.47224 StartZ=0 EndX=1.275 EndY=-0.736122 EndZ=0
    g5: LineSegment StartX=1.275 StartY=-0.736122 StartZ=0 EndX=1.275 EndY=0.736122 EndZ=0
    g6: Circle [constr] CenterX=0 CenterY=0 CenterZ=0 NormalX=0 NormalY=0 NormalZ=1 AngleXU=0 Radius=1.47224
  constraints (16):
    c: Coincident(g0,g1)
    c: Coincident(g1,g2)
    c: Coincident(g2,g3)
    c: Coincident(g3,g4)
    c: Coincident(g4,g5)
    c: Coincident(g5,g0)
    c: Equal(g0, g1-g5) x5
    c: PointOnObject(g0,g6)
    c: PointOnObject(g1,g6)
    c: PointOnObject(g2,g6)
    c: PointOnObject(g3,g6)
    c: PointOnObject(g4,g6)
    c: PointOnObject(g5,g6)
    c: Coincident(g6,g-1)
    c: PointOnObject(g0,g-2)
    c: DistanceX(g1,g0) = 2.55
FEATURE [PartDesign::Pocket] Pocket184  label="M3x8 Wrench015"
  BaseFeature = -> Pad155
  Length = 1.3
  Length2 = 100
  Profile = -> Sketch409
  Type = 0
FEATURE [PartDesign::Chamfer] Chamfer062  label="M3x8 Smooth015"
  Base = -> Pocket184 [Face11,Edge2,Edge24,Edge3]
  BaseFeature = -> Pocket184
  Size = 0.2
FEATURE [PartDesign::Body] Body086  label="M3x021"
  Group = -> [Sketch408,Pad156,Sketch410,Pad155,Sketch409,Pocket184,Chamfer062]
  Origin = -> Origin123
  Placement = pos=(-144.1,-31.4,27.05) rot=(-1,0,0;1.5708rad)
  Tip = -> Chamfer062
FEATURE [Sketcher::SketchObject] Sketch572
  MapMode = 5
  Support = -> [XY_Plane217]
FEATURE [Sketcher::SketchObject] Sketch573
  MapMode = 5
  Support = -> [XY_Plane217]
FEATURE [Sketcher::SketchObject] Sketch574
  MapMode = 5
  Support = -> [XY_Plane218]
  sketch-geometry (2):
    g0: Circle CenterX=0 CenterY=0 CenterZ=0 NormalX=0 NormalY=0 NormalZ=1 AngleXU=0 Radius=2.5
    g1: Circle CenterX=0 CenterY=0 CenterZ=0 NormalX=0 NormalY=0 NormalZ=1 AngleXU=0 Radius=1
  constraints (4):
    c: Coincident(g0,g-1)
    c: Coincident(g1,g0)
    c: Radius(g0) = 2.5
    c: Radius(g1) = 1
FEATURE [Sketcher::SketchObject] Sketch576
  MapMode = 5
  Support = -> [XY_Plane214]
  sketch-geometry (8):
    g0: LineSegment StartX=0 StartY=2.3094 StartZ=0 EndX=-2 EndY=1.1547 EndZ=0
    g1: LineSegment StartX=-2 StartY=1.1547 StartZ=0 EndX=-2 EndY=-1.1547 EndZ=0
    g2: LineSegment StartX=-2 StartY=-1.1547 StartZ=0 EndX=-2e-16 EndY=-2.3094 EndZ=0
    g3: LineSegment StartX=-2e-16 StartY=-2.3094 StartZ=0 EndX=2 EndY=-1.1547 EndZ=0
    g4: LineSegment StartX=2 StartY=-1.1547 StartZ=0 EndX=2 EndY=1.1547 EndZ=0
    g5: LineSegment StartX=2 StartY=1.1547 StartZ=0 EndX=0 EndY=2.3094 EndZ=0
    g6: Circle [constr] CenterX=0 CenterY=0 CenterZ=0 NormalX=0 NormalY=0 NormalZ=1 AngleXU=0 Radius=2.3094
    g7: Circle CenterX=0 CenterY=0 CenterZ=0 NormalX=0 NormalY=0 NormalZ=1 AngleXU=0 Radius=1
  constraints (18):
    c: Coincident(g0,g1)
    c: Coincident(g1,g2)
    c: Coincident(g2,g3)
    c: Coincident(g3,g4)
    c: Coincident(g4,g5)
    c: Coincident(g5,g0)
    c: Equal(g0, g1-g5) x5
    c: PointOnObject(g0,g6)
    c: PointOnObject(g1,g6)
    c: PointOnObject(g2,g6)
    c: PointOnObject(g3,g6)
    c: PointOnObject(g4,g6)
    c: PointOnObject(g5,g6)
    c: Coincident(g6,g-1)
    c: PointOnObject(g5,g-2)
    c: DistanceX(g0,g4) = 4
    c: Coincident(g7,g-1)
    c: Radius(g7) = 1
FEATURE [PartDesign::Pad] Pad230  label="Ball Bearing Pin001"
  Length = 5
  Length2 = 100
  Profile = -> Sketch574
  Type = 0
FEATURE [PartDesign::Chamfer] Chamfer116  label="Smooth Pinhead001"
  Base = -> Pad230 [Edge3]
  BaseFeature = -> Pad230
  Size = 0.4
FEATURE [PartDesign::Pad] Pad242  label="M3 Nut Primitive044"
  Length = 0.6
  Length2 = 0.6
  Profile = -> Sketch576
  Type = 4
FEATURE [Sketcher::SketchObject] Sketch588
  MapMode = 5
  Support = -> [XY_Plane001]
  sketch-geometry (8):
    g0: LineSegment StartX=-16.75 StartY=28.25 StartZ=0 EndX=16.75 EndY=28.25 EndZ=0
    g1: LineSegment StartX=21.75 StartY=23.25 StartZ=0 EndX=21.75 EndY=-23.25 EndZ=0
    g2: LineSegment StartX=16.75 StartY=-28.25 StartZ=0 EndX=-16.75 EndY=-28.25 EndZ=0
    g3: LineSegment StartX=-21.75 StartY=-23.25 StartZ=0 EndX=-21.75 EndY=23.25 EndZ=0
    g4: ArcOfCircle CenterX=-16.75 CenterY=23.25 CenterZ=0 NormalX=0 NormalY=0 NormalZ=1 AngleXU=0 Radius=5 StartAngle=1.5708 EndAngle=3.14159
    g5: ArcOfCircle CenterX=16.75 CenterY=23.25 CenterZ=0 NormalX=0 NormalY=0 NormalZ=1 AngleXU=0 Radius=5 StartAngle=1e-16 EndAngle=1.5708
    g6: ArcOfCircle CenterX=16.75 CenterY=-23.25 CenterZ=0 NormalX=0 NormalY=0 NormalZ=1 AngleXU=0 Radius=5 StartAngle=4.71239 EndAngle=6.28319
    g7: ArcOfCircle CenterX=-16.75 CenterY=-23.25 CenterZ=0 NormalX=0 NormalY=0 NormalZ=1 AngleXU=0 Radius=5 StartAngle=3.14159 EndAngle=4.71239
  constraints (18):
    c: Horizontal(g2)
    c: Vertical(g1)
    c: Tangent(g3,g4) = 1.5708
    c: Tangent(g0,g4) = 1.5708
    c: Tangent(g0,g5) = 1.5708
    c: Tangent(g1,g5) = 1.5708
    c: Tangent(g1,g6) = 1.5708
    c: Tangent(g2,g6) = 1.5708
    c: Tangent(g2,g7) = 1.5708
    c: Tangent(g3,g7) = 1.5708
    c: Equal(g4,g5)
    c: Equal(g5,g7)
    c: Equal(g7,g6)
    c: Radius(g5) = 5
    c: DistanceY(g2,g0) = 56.5
    c: DistanceX(g3,g1) = 43.5
    c: Symmetric(g0,g0,g-2)
    c: Symmetric(g3,g3,g-1)
FEATURE [Sketcher::SketchObject] Sketch593
  MapMode = 5
  Support = -> [XY_Plane002]
  sketch-geometry (13):
    g0: Circle [constr] CenterX=0 CenterY=0 CenterZ=0 NormalX=0 NormalY=0 NormalZ=1 AngleXU=0 Radius=20
    g1: LineSegment [constr] StartX=-14.1421 StartY=14.1421 StartZ=0 EndX=14.1421 EndY=14.1421 EndZ=0
    g2: LineSegment [constr] StartX=14.1421 StartY=14.1421 StartZ=0 EndX=14.1421 EndY=-14.1421 EndZ=0
    g3: LineSegment [constr] StartX=14.1421 StartY=-14.1421 StartZ=0 EndX=-14.1421 EndY=-14.1421 EndZ=0
    g4: LineSegment [constr] StartX=-14.1421 StartY=-14.1421 StartZ=0 EndX=-14.1421 EndY=14.1421 EndZ=0
    g5: ArcOfCircle CenterX=0 CenterY=0 CenterZ=0 NormalX=0 NormalY=0 NormalZ=1 AngleXU=0 Radius=20 StartAngle=2.60685 EndAngle=3.67634
    g6: ArcOfCircle CenterX=-14.1421 CenterY=14.1421 CenterZ=0 NormalX=0 NormalY=0 NormalZ=1 AngleXU=0 Radius=5 StartAngle=0.66007 EndAngle=4.05232
    g7: ArcOfCircle CenterX=14.1421 CenterY=14.1421 CenterZ=0 NormalX=0 NormalY=0 NormalZ=1 AngleXU=0 Radius=5 StartAngle=5.37246 EndAngle=8.76471
    g8: ArcOfCircle CenterX=14.1421 CenterY=-14.1421 CenterZ=0 NormalX=0 NormalY=0 NormalZ=1 AngleXU=0 Radius=5 StartAngle=3.80166 EndAngle=7.19391
    g9: ArcOfCircle CenterX=-14.1421 CenterY=-14.1421 CenterZ=0 NormalX=0 NormalY=0 NormalZ=1 AngleXU=0 Radius=5 StartAngle=2.23087 EndAngle=5.62311
    g10: ArcOfCircle CenterX=0 CenterY=0 CenterZ=0 NormalX=0 NormalY=0 NormalZ=1 AngleXU=0 Radius=20 StartAngle=1.03605 EndAngle=2.10554
    g11: ArcOfCircle CenterX=0 CenterY=0 CenterZ=0 NormalX=0 NormalY=0 NormalZ=1 AngleXU=0 Radius=20 StartAngle=5.74844 EndAngle=6.81793
    g12: ArcOfCircle CenterX=0 CenterY=0 CenterZ=0 NormalX=0 NormalY=0 NormalZ=1 AngleXU=0 Radius=20 StartAngle=4.17765 EndAngle=5.24713
  constraints (38):
    c: Coincident(g0,g-1)
    c: Radius(g0) = 20
    c: Coincident(g1,g2)
    c: Coincident(g2,g3)
    c: Coincident(g3,g4)
    c: Coincident(g4,g1)
    c: Horizontal(g1)
    c: Horizontal(g3)
    c: Vertical(g2)
    c: Vertical(g4)
    c: PointOnObject(g1,g0)
    c: PointOnObject(g2,g0)
    c: Equal(g1,g2)
    c: PointOnObject(g1,g0)
    c: Coincident(g5,g-1)
    c: Radius(g5) = 20
    c: Coincident(g6,g1)
    c: Coincident(g7,g1)
    c: Coincident(g8,g2)
    c: Coincident(g9,g3)
    c: Coincident(g5,g6)
    c: Equal(g5,g10)
    c: Coincident(g10,g7)
    c: Coincident(g5,g10)
    c: Coincident(g11,g7)
    c: Equal(g5,g11)
    c: Coincident(g11,g8)
    c: Coincident(g5,g11)
    c: Coincident(g12,g8)
    c: Equal(g5,g12)
    c: Coincident(g12,g9)
    c: Coincident(g5,g12)
    c: Coincident(g5,g9)
    c: Coincident(g6,g10)
    c: Radius(g6) = 5
    c: Equal(g6,g7)
    c: Equal(g6,g8)
    c: Equal(g6,g9)
FEATURE [Sketcher::SketchObject] Sketch595
  MapMode = 5
  Support = -> [XY_Plane198]
  sketch-geometry (64):
    g0: LineSegment [constr] StartX=-3.75 StartY=6.49519 StartZ=0 EndX=-7.5 EndY=0 EndZ=0
    g1: LineSegment [constr] StartX=-7.5 StartY=0 StartZ=0 EndX=-3.75 EndY=-6.49519 EndZ=0
    g2: LineSegment [constr] StartX=-3.75 StartY=-6.49519 StartZ=0 EndX=3.75 EndY=-6.49519 EndZ=0
    g3: LineSegment [constr] StartX=3.75 StartY=-6.49519 StartZ=0 EndX=7.5 EndY=0 EndZ=0
    g4: LineSegment [constr] StartX=7.5 StartY=0 StartZ=0 EndX=3.75 EndY=6.49519 EndZ=0
    g5: LineSegment [constr] StartX=3.75 StartY=6.49519 StartZ=0 EndX=-3.75 EndY=6.49519 EndZ=0
    g6: Circle [constr] CenterX=0 CenterY=0 CenterZ=0 NormalX=0 NormalY=0 NormalZ=1 AngleXU=0 Radius=7.5
    g7: LineSegment [constr] StartX=0 StartY=7.5 StartZ=0 EndX=-6.49519 EndY=3.75 EndZ=0
    g8: LineSegment [constr] StartX=-6.49519 StartY=3.75 StartZ=0 EndX=-6.49519 EndY=-3.75 EndZ=0
    g9: LineSegment [constr] StartX=-6.49519 StartY=-3.75 StartZ=0 EndX=9.8e-15 EndY=-7.5 EndZ=0
    g10: LineSegment [constr] StartX=9.8e-15 StartY=-7.5 StartZ=0 EndX=6.49519 EndY=-3.75 EndZ=0
    g11: LineSegment [constr] StartX=6.49519 StartY=-3.75 StartZ=0 EndX=6.49519 EndY=3.75 EndZ=0
    g12: LineSegment [constr] StartX=6.49519 StartY=3.75 StartZ=0 EndX=0 EndY=7.5 EndZ=0
    g13: Circle [constr] CenterX=0 CenterY=0 CenterZ=0 NormalX=0 NormalY=0 NormalZ=1 AngleXU=0 Radius=7.5
    g14: LineSegment [constr] StartX=0 StartY=10.5 StartZ=0 EndX=-9.09327 EndY=5.25 EndZ=0
    g15: LineSegment [constr] StartX=-9.09327 StartY=5.25 StartZ=0 EndX=-9.09327 EndY=-5.25 EndZ=0
    g16: LineSegment [constr] StartX=-9.09327 StartY=-5.25 StartZ=0 EndX=-1.42e-14 EndY=-10.5 EndZ=0
    g17: LineSegment [constr] StartX=-1.42e-14 StartY=-10.5 StartZ=0 EndX=9.09327 EndY=-5.25 EndZ=0
    g18: LineSegment [constr] StartX=9.09327 StartY=-5.25 StartZ=0 EndX=9.09327 EndY=5.25 EndZ=0
    g19: LineSegment [constr] StartX=9.09327 StartY=5.25 StartZ=0 EndX=0 EndY=10.5 EndZ=0
    g20: Circle [constr] CenterX=0 CenterY=0 CenterZ=0 NormalX=0 NormalY=0 NormalZ=1 AngleXU=0 Radius=10.5
    g21: LineSegment [constr] StartX=0 StartY=13.5 StartZ=0 EndX=-11.6913 EndY=6.75 EndZ=0
    g22: LineSegment [constr] StartX=-11.6913 StartY=6.75 StartZ=0 EndX=-11.6913 EndY=-6.75 EndZ=0
    g23: LineSegment [constr] StartX=-11.6913 StartY=-6.75 StartZ=0 EndX=0 EndY=-13.5 EndZ=0
    g24: LineSegment [constr] StartX=0 StartY=-13.5 StartZ=0 EndX=11.6913 EndY=-6.75 EndZ=0
    g25: LineSegment [constr] StartX=11.6913 StartY=-6.75 StartZ=0 EndX=11.6913 EndY=6.75 EndZ=0
    g26: LineSegment [constr] StartX=11.6913 StartY=6.75 StartZ=0 EndX=0 EndY=13.5 EndZ=0
    g27: Circle [constr] CenterX=0 CenterY=0 CenterZ=0 NormalX=0 NormalY=0 NormalZ=1 AngleXU=0 Radius=13.5
    g28: ArcOfCircle CenterX=0 CenterY=13.5 CenterZ=0 NormalX=0 NormalY=0 NormalZ=1 AngleXU=0 Radius=2.5 StartAngle=0.171439 EndAngle=2.97015
    g29: ArcOfCircle CenterX=11.6913 CenterY=6.75 CenterZ=0 NormalX=0 NormalY=0 NormalZ=1 AngleXU=0 Radius=2.5 StartAngle=5.40743 EndAngle=8.20614
    g30: ArcOfCircle CenterX=11.6913 CenterY=-6.75 CenterZ=0 NormalX=0 NormalY=0 NormalZ=1 AngleXU=0 Radius=2.5 StartAngle=4.36023 EndAngle=7.15894
    g31: ArcOfCircle CenterX=0 CenterY=-13.5 CenterZ=0 NormalX=0 NormalY=0 NormalZ=1 AngleXU=0 Radius=2.5 StartAngle=3.31303 EndAngle=6.11175
    g32: ArcOfCircle CenterX=-11.6913 CenterY=-6.75 CenterZ=0 NormalX=0 NormalY=0 NormalZ=1 AngleXU=0 Radius=2.5 StartAngle=2.26583 EndAngle=5.06455
    g33: ArcOfCircle CenterX=-11.6913 CenterY=6.75 CenterZ=0 NormalX=0 NormalY=0 NormalZ=1 AngleXU=0 Radius=2.5 StartAngle=1.21864 EndAngle=4.01735
    g34: LineSegment StartX=-10.829 StartY=9.09658 StartZ=0 EndX=-3.75 EndY=6.49519 EndZ=0
    g35: LineSegment StartX=-3.75 StartY=6.49519 StartZ=0 EndX=-2.46335 EndY=13.9265 EndZ=0
    g36: LineSegment StartX=2.46335 StartY=13.9265 StartZ=0 EndX=3.75 EndY=6.49519 EndZ=0
    g37: LineSegment StartX=3.75 StartY=6.49519 StartZ=0 EndX=10.829 EndY=9.09658 EndZ=0
    g38: LineSegment StartX=13.2924 StartY=4.82993 StartZ=0 EndX=7.5 EndY=0 EndZ=0
    g39: LineSegment StartX=7.5 StartY=0 StartZ=0 EndX=13.2924 EndY=-4.82993 EndZ=0
    g40: LineSegment StartX=10.829 StartY=-9.09658 StartZ=0 EndX=3.75 EndY=-6.49519 EndZ=0
    g41: LineSegment StartX=3.75 StartY=-6.49519 StartZ=0 EndX=2.46335 EndY=-13.9265 EndZ=0
    g42: LineSegment StartX=-2.46335 StartY=-13.9265 StartZ=0 EndX=-3.75 EndY=-6.49519 EndZ=0
    g43: LineSegment StartX=-3.75 StartY=-6.49519 StartZ=0 EndX=-10.829 EndY=-9.09658 EndZ=0
    g44: LineSegment StartX=-13.2924 StartY=-4.82993 StartZ=0 EndX=-7.5 EndY=0 EndZ=0
    g45: LineSegment StartX=-7.5 StartY=0 StartZ=0 EndX=-13.2924 EndY=4.82993 EndZ=0
    g46: Circle CenterX=-11.6913 CenterY=6.75 CenterZ=0 NormalX=0 NormalY=0 NormalZ=1 AngleXU=0 Radius=0.75
    g47: Circle CenterX=-9.09327 CenterY=5.25 CenterZ=0 NormalX=0 NormalY=0 NormalZ=1 AngleXU=0 Radius=0.75
    g48: Circle CenterX=-6.49519 CenterY=3.75 CenterZ=0 NormalX=0 NormalY=0 NormalZ=1 AngleXU=0 Radius=0.75
    g49: Circle CenterX=0 CenterY=13.5 CenterZ=0 NormalX=0 NormalY=0 NormalZ=1 AngleXU=0 Radius=0.75
    g50: Circle CenterX=0 CenterY=10.5 CenterZ=0 NormalX=0 NormalY=0 NormalZ=1 AngleXU=0 Radius=0.75
    g51: Circle CenterX=0 CenterY=7.5 CenterZ=0 NormalX=0 NormalY=0 NormalZ=1 AngleXU=0 Radius=0.75
    g52: Circle CenterX=11.6913 CenterY=6.75 CenterZ=0 NormalX=0 NormalY=0 NormalZ=1 AngleXU=0 Radius=0.75
    g53: Circle CenterX=9.09327 CenterY=5.25 CenterZ=0 NormalX=0 NormalY=0 NormalZ=1 AngleXU=0 Radius=0.75
    g54: Circle CenterX=6.49519 CenterY=3.75 CenterZ=0 NormalX=0 NormalY=0 NormalZ=1 AngleXU=0 Radius=0.75
    g55: Circle CenterX=11.6913 CenterY=-6.75 CenterZ=0 NormalX=0 NormalY=0 NormalZ=1 AngleXU=0 Radius=0.75
    g56: Circle CenterX=9.09327 CenterY=-5.25 CenterZ=0 NormalX=0 NormalY=0 NormalZ=1 AngleXU=0 Radius=0.75
    g57: Circle CenterX=6.49519 CenterY=-3.75 CenterZ=0 NormalX=0 NormalY=0 NormalZ=1 AngleXU=0 Radius=0.75
    g58: Circle CenterX=9.8e-15 CenterY=-7.5 CenterZ=0 NormalX=0 NormalY=0 NormalZ=1 AngleXU=0 Radius=0.75
    g59: Circle CenterX=-1.42e-14 CenterY=-10.5 CenterZ=0 NormalX=0 NormalY=0 NormalZ=1 AngleXU=0 Radius=0.75
    g60: Circle CenterX=0 CenterY=-13.5 CenterZ=0 NormalX=0 NormalY=0 NormalZ=1 AngleXU=0 Radius=0.75
    g61: Circle CenterX=-11.6913 CenterY=-6.75 CenterZ=0 NormalX=0 NormalY=0 NormalZ=1 AngleXU=0 Radius=0.75
    g62: Circle CenterX=-9.09327 CenterY=-5.25 CenterZ=0 NormalX=0 NormalY=0 NormalZ=1 AngleXU=0 Radius=0.75
    g63: Circle CenterX=-6.49519 CenterY=-3.75 CenterZ=0 NormalX=0 NormalY=0 NormalZ=1 AngleXU=0 Radius=0.75
  constraints (136):
    c: Coincident(g0,g1)
    c: Coincident(g1,g2)
    c: Coincident(g2,g3)
    c: Coincident(g3,g4)
    c: Coincident(g4,g5)
    c: Coincident(g5,g0)
    c: Equal(g0, g1-g5) x5
    c: PointOnObject(g0,g6)
    c: PointOnObject(g1,g6)
    c: PointOnObject(g2,g6)
    c: PointOnObject(g3,g6)
    c: PointOnObject(g4,g6)
    c: PointOnObject(g5,g6)
    c: Coincident(g6,g-1)
    c: Coincident(g7,g8)
    c: Coincident(g8,g9)
    c: Coincident(g9,g10)
    c: Coincident(g10,g11)
    c: Coincident(g11,g12)
    c: Coincident(g12,g7)
    c: Equal(g7, g8-g12) x5
    c: PointOnObject(g7,g13)
    c: PointOnObject(g8,g13)
    c: PointOnObject(g9,g13)
    c: PointOnObject(g10,g13)
    c: PointOnObject(g11,g13)
    c: PointOnObject(g12,g13)
    c: Coincident(g13,g-1)
    c: PointOnObject(g12,g6)
    c: PointOnObject(g7,g-2)
    c: Horizontal(g5)
    c: Radius(g6) = 7.5
    c: Coincident(g14,g15)
    c: Coincident(g15,g16)
    c: Coincident(g16,g17)
    c: Coincident(g17,g18)
    c: Coincident(g18,g19)
    c: Coincident(g19,g14)
    c: Equal(g14, g15-g19) x5
    c: PointOnObject(g14,g20)
    c: PointOnObject(g15,g20)
    c: PointOnObject(g16,g20)
    c: PointOnObject(g17,g20)
    c: PointOnObject(g18,g20)
    c: PointOnObject(g19,g20)
    c: Coincident(g20,g-1)
    c: PointOnObject(g19,g-2)
    c: Radius(g20) = 10.5
    c: Coincident(g21,g22)
    c: Coincident(g22,g23)
    c: Coincident(g23,g24)
    c: Coincident(g24,g25)
    c: Coincident(g25,g26)
    c: Coincident(g26,g21)
    c: Equal(g21, g22-g26) x5
    c: PointOnObject(g21,g27)
    c: PointOnObject(g22,g27)
    c: PointOnObject(g23,g27)
    c: PointOnObject(g24,g27)
    c: PointOnObject(g25,g27)
    c: PointOnObject(g26,g27)
    c: Coincident(g27,g-1)
    c: PointOnObject(g26,g-2)
    c: Radius(g27) = 13.5
    c: Coincident(g28,g21)
    c: Coincident(g29,g25)
    c: Coincident(g30,g24)
    c: Coincident(g31,g23)
    c: Coincident(g32,g22)
    c: Coincident(g33,g21)
    c: Coincident(g34,g0)
    c: Coincident(g35,g34)
    c: Coincident(g36,g4)
    c: Coincident(g37,g36)
    c: Coincident(g38,g3)
    c: Coincident(g39,g38)
    c: Coincident(g40,g2)
    c: Coincident(g41,g40)
    c: Coincident(g42,g1)
    c: Coincident(g43,g42)
    c: Coincident(g44,g0)
    c: Coincident(g45,g44)
    c: Tangent(g35,g28) = 1.5708
    c: Tangent(g36,g28) = 1.5708
    c: Tangent(g37,g29) = 1.5708
    c: Tangent(g38,g29) = 1.5708
    c: Tangent(g39,g30) = 1.5708
    c: Tangent(g40,g30) = 1.5708
    c: Tangent(g41,g31) = 1.5708
    c: Tangent(g42,g31) = 1.5708
    c: Tangent(g43,g32) = 1.5708
    c: Tangent(g44,g32) = 1.5708
    c: Tangent(g45,g33) = 1.5708
    c: Tangent(g34,g33) = 1.5708
    c: Radius(g29) = 2.5
    c: Equal(g29,g28)
    c: Equal(g28,g33)
    c: Equal(g33,g32)
    c: Equal(g32,g31)
    c: Equal(g31,g30)
    c: Coincident(g46,g33)
    c: Coincident(g47,g14)
    c: Coincident(g48,g7)
    c: Coincident(g49,g28)
    c: Coincident(g50,g14)
    c: Coincident(g51,g7)
    c: Coincident(g52,g29)
    c: Coincident(g53,g18)
    c: Coincident(g54,g11)
    c: Coincident(g55,g30)
    c: Coincident(g56,g17)
    c: Coincident(g57,g10)
    c: Coincident(g58,g9)
    c: Coincident(g59,g16)
    c: Coincident(g60,g31)
    c: Coincident(g61,g32)
    c: Coincident(g62,g15)
    c: Coincident(g63,g8)
    c: Equal(g61,g62)
    c: Equal(g62,g63)
    c: Equal(g63,g58)
    c: Equal(g58,g59)
    c: Equal(g59,g60)
    c: Equal(g60,g55)
    c: Equal(g55,g56)
    c: Equal(g56,g57)
    c: Equal(g57,g54)
    c: Equal(g54,g53)
    c: Equal(g53,g52)
    c: Equal(g52,g51)
    c: Equal(g51,g50)
    c: Equal(g50,g49)
    c: Equal(g49,g46)
    c: Equal(g46,g47)
    c: Equal(g47,g48)
    c: Radius(g55) = 0.75
FEATURE [PartDesign::Pad] Pad237
  Length = 2
  Length2 = 100
  Profile = -> Sketch595
  Type = 0
FEATURE [Sketcher::SketchObject] Sketch589
  MapMode = 5
  Placement = pos=(0,0,2) rot=(0,0,1;0rad)
  Support = -> [Pad237]
  sketch-geometry (2):
    g0: Circle CenterX=0 CenterY=0 CenterZ=0 NormalX=0 NormalY=0 NormalZ=1 AngleXU=0 Radius=5
    g1: Circle CenterX=0 CenterY=0 CenterZ=0 NormalX=0 NormalY=0 NormalZ=1 AngleXU=0 Radius=3.5
  constraints (4):
    c: Coincident(g0,g-1)
    c: Coincident(g1,g0)
    c: Radius(g1) = 3.5
    c: Radius(g0) = 5
FEATURE [PartDesign::Pocket] Pocket257
  BaseFeature = -> Pad237
  Length = 1
  Length2 = 100
  Profile = -> Sketch589
  Type = 0
FEATURE [Sketcher::SketchObject] Sketch580
  MapMode = 5
  Placement = pos=(0,0,2) rot=(0,0,1;0rad)
  Support = -> [Pocket257]
  sketch-geometry (1):
    g0: Circle CenterX=0 CenterY=0 CenterZ=0 NormalX=0 NormalY=0 NormalZ=1 AngleXU=0 Radius=3
  constraints (2):
    c: Coincident(g0,g-1)
    c: Radius(g0) = 3
FEATURE [PartDesign::Pocket] Pocket260
  BaseFeature = -> Pocket257
  Length = 1
  Length2 = 100
  Profile = -> Sketch580
  Type = 0
FEATURE [Sketcher::SketchObject] Sketch579
  MapMode = 5
  Placement = pos=(0,0,1) rot=(0,0,1;0rad)
  Support = -> [Pocket260]
  sketch-geometry (1):
    g0: Circle CenterX=0 CenterY=0 CenterZ=0 NormalX=0 NormalY=0 NormalZ=1 AngleXU=0 Radius=1.5
  constraints (2):
    c: Coincident(g0,g-1)
    c: Radius(g0) = 1.5
FEATURE [PartDesign::Pocket] Pocket256
  BaseFeature = -> Pocket260
  Length = 5
  Length2 = 100
  Profile = -> Sketch579
  Type = 0
FEATURE [Sketcher::SketchObject] Sketch594
  MapMode = 5
  Placement = pos=(0,0,0) rot=(1,0,0;3.14159rad)
  Support = -> [Pocket256]
  sketch-geometry (2):
    g0: Circle CenterX=0 CenterY=0 CenterZ=0 NormalX=0 NormalY=0 NormalZ=1 AngleXU=0 Radius=4.5
    g1: Circle CenterX=0 CenterY=0 CenterZ=0 NormalX=0 NormalY=0 NormalZ=1 AngleXU=0 Radius=3
  constraints (4):
    c: Coincident(g0,g-1)
    c: Coincident(g1,g0)
    c: Radius(g0) = 4.5
    c: Radius(g1) = 3
FEATURE [PartDesign::Pad] Pad236
  BaseFeature = -> Pocket256
  Length = 3
  Length2 = 100
  Profile = -> Sketch594
  Type = 0
FEATURE [PartDesign::Fillet] Fillet083
  Base = -> Pad236 [Face5,Edge96,Face4]
  BaseFeature = -> Pad236
  Radius = 0.2
FEATURE [PartDesign::Body] Body143  label="Shoulder_Joint_Ball_Bearing_Pin001"
  Group = -> [Sketch574,Pad230,Chamfer116]
  Origin = -> Origin191
  Placement = pos=(-21.75,10,15) rot=(0,-1,0;1.5708rad)
  Tip = -> Chamfer116
FEATURE [Sketcher::SketchObject] Sketch599
  MapMode = 5
  Support = -> [XY_Plane199]
FEATURE [Sketcher::SketchObject] Sketch600
  MapMode = 5
  Support = -> [XY_Plane199]
FEATURE [Sketcher::SketchObject] Sketch601
  MapMode = 5
  Support = -> [XY_Plane213]
  sketch-geometry (1):
    g0: Circle CenterX=0 CenterY=0 CenterZ=0 NormalX=0 NormalY=0 NormalZ=1 AngleXU=0 Radius=1.9
  constraints (2):
    c: Coincident(g0,g-1)
    c: Radius(g0) = 1.9
FEATURE [PartDesign::Pad] Pad234  label="M3x8 Head026"
  Length = 2
  Length2 = 100
  Profile = -> Sketch601
  Type = 0
FEATURE [Sketcher::SketchObject] Sketch602
  MapMode = 5
  Support = -> [XY_Plane217]
  sketch-geometry (8):
    g0: LineSegment StartX=0 StartY=2.3094 StartZ=0 EndX=-2 EndY=1.1547 EndZ=0
    g1: LineSegment StartX=-2 StartY=1.1547 StartZ=0 EndX=-2 EndY=-1.1547 EndZ=0
    g2: LineSegment StartX=-2 StartY=-1.1547 StartZ=0 EndX=-2e-16 EndY=-2.3094 EndZ=0
    g3: LineSegment StartX=-2e-16 StartY=-2.3094 StartZ=0 EndX=2 EndY=-1.1547 EndZ=0
    g4: LineSegment StartX=2 StartY=-1.1547 StartZ=0 EndX=2 EndY=1.1547 EndZ=0
    g5: LineSegment StartX=2 StartY=1.1547 StartZ=0 EndX=0 EndY=2.3094 EndZ=0
    g6: Circle [constr] CenterX=0 CenterY=0 CenterZ=0 NormalX=0 NormalY=0 NormalZ=1 AngleXU=0 Radius=2.3094
    g7: Circle CenterX=0 CenterY=0 CenterZ=0 NormalX=0 NormalY=0 NormalZ=1 AngleXU=0 Radius=1
  constraints (18):
    c: Coincident(g0,g1)
    c: Coincident(g1,g2)
    c: Coincident(g2,g3)
    c: Coincident(g3,g4)
    c: Coincident(g4,g5)
    c: Coincident(g5,g0)
    c: Equal(g0, g1-g5) x5
    c: PointOnObject(g0,g6)
    c: PointOnObject(g1,g6)
    c: PointOnObject(g2,g6)
    c: PointOnObject(g3,g6)
    c: PointOnObject(g4,g6)
    c: PointOnObject(g5,g6)
    c: Coincident(g6,g-1)
    c: PointOnObject(g5,g-2)
    c: DistanceX(g0,g4) = 4
    c: Coincident(g7,g-1)
    c: Radius(g7) = 1
FEATURE [PartDesign::Pad] Pad238  label="M3 Nut Primitive042"
  Length = 0.6
  Length2 = 0.6
  Profile = -> Sketch602
  Type = 4
FEATURE [Sketcher::SketchObject] Sketch603
  MapMode = 5
  Support = -> [XY_Plane216]
  sketch-geometry (1):
    g0: Circle CenterX=0 CenterY=0 CenterZ=0 NormalX=0 NormalY=0 NormalZ=1 AngleXU=0 Radius=1.9
  constraints (2):
    c: Coincident(g0,g-1)
    c: Radius(g0) = 1.9
FEATURE [PartDesign::Pad] Pad239  label="M3x8 Head027"
  Length = 2
  Length2 = 100
  Profile = -> Sketch603
  Type = 0
FEATURE [Sketcher::SketchObject] Sketch604
  MapMode = 5
  Support = -> [XY_Plane205]
  sketch-geometry (1):
    g0: Circle CenterX=0 CenterY=0 CenterZ=0 NormalX=0 NormalY=0 NormalZ=1 AngleXU=0 Radius=1.9
  constraints (2):
    c: Coincident(g0,g-1)
    c: Radius(g0) = 1.9
FEATURE [PartDesign::Pad] Pad233  label="M3x8 Head025"
  Length = 2
  Length2 = 100
  Profile = -> Sketch604
  Type = 0
FEATURE [Sketcher::SketchObject] Sketch606
  MapMode = 5
  Placement = pos=(0,0,2) rot=(0,0,1;0rad)
  Support = -> [Pad239]
  sketch-geometry (1):
    g0: Circle CenterX=0 CenterY=0 CenterZ=0 NormalX=0 NormalY=0 NormalZ=1 AngleXU=0 Radius=1
  constraints (2):
    c: Coincident(g0,g-1)
    c: Radius(g0) = 1
FEATURE [PartDesign::Pad] Pad246  label="M3x8 Thread029"
  BaseFeature = -> Pad239
  Length = 8
  Length2 = 100
  Profile = -> Sketch606
  Type = 0
FEATURE [Sketcher::SketchObject] Sketch605
  MapMode = 5
  Placement = pos=(0,0,0) rot=(1,0,0;3.14159rad)
  Support = -> [Pad246]
  sketch-geometry (7):
    g0: LineSegment StartX=0.77 StartY=0.44456 StartZ=0 EndX=0 EndY=0.889119 EndZ=0
    g1: LineSegment StartX=0 StartY=0.889119 StartZ=0 EndX=-0.77 EndY=0.44456 EndZ=0
    g2: LineSegment StartX=-0.77 StartY=0.44456 StartZ=0 EndX=-0.77 EndY=-0.44456 EndZ=0
    g3: LineSegment StartX=-0.77 StartY=-0.44456 StartZ=0 EndX=3.85628e-11 EndY=-0.889119 EndZ=0
    g4: LineSegment StartX=3.85628e-11 StartY=-0.889119 StartZ=0 EndX=0.77 EndY=-0.44456 EndZ=0
    g5: LineSegment StartX=0.77 StartY=-0.44456 StartZ=0 EndX=0.77 EndY=0.44456 EndZ=0
    g6: Circle [constr] CenterX=0 CenterY=0 CenterZ=0 NormalX=0 NormalY=0 NormalZ=1 AngleXU=0 Radius=0.889119
  constraints (16):
    c: Coincident(g0,g1)
    c: Coincident(g1,g2)
    c: Coincident(g2,g3)
    c: Coincident(g3,g4)
    c: Coincident(g4,g5)
    c: Coincident(g5,g0)
    c: Equal(g0, g1-g5) x5
    c: PointOnObject(g0,g6)
    c: PointOnObject(g1,g6)
    c: PointOnObject(g2,g6)
    c: PointOnObject(g3,g6)
    c: PointOnObject(g4,g6)
    c: PointOnObject(g5,g6)
    c: Coincident(g6,g-1)
    c: PointOnObject(g0,g-2)
    c: DistanceX(g1,g0) = 1.54
FEATURE [PartDesign::Pocket] Pocket258  label="M3x8 Wrench025"
  BaseFeature = -> Pad246
  Length = 1
  Length2 = 100
  Profile = -> Sketch605
  Type = 0
FEATURE [PartDesign::Chamfer] Chamfer114  label="M3x8 Smooth032"
  Base = -> Pocket258 [Face11,Edge2,Edge24,Edge3]
  BaseFeature = -> Pocket258
  Size = 0.2
FEATURE [PartDesign::Body] Body139  label="M2x028"
  Group = -> [Sketch603,Pad239,Sketch606,Pad246,Sketch605,Pocket258,Chamfer114]
  Origin = -> Origin203
  Tip = -> Chamfer114
FEATURE [Sketcher::SketchObject] Sketch607
  MapMode = 5
  Support = -> [XY_Plane201]
FEATURE [Sketcher::SketchObject] Sketch609
  MapMode = 5
  Support = -> [XY_Plane199]
  sketch-geometry (8):
    g0: LineSegment StartX=0 StartY=2.3094 StartZ=0 EndX=-2 EndY=1.1547 EndZ=0
    g1: LineSegment StartX=-2 StartY=1.1547 StartZ=0 EndX=-2 EndY=-1.1547 EndZ=0
    g2: LineSegment StartX=-2 StartY=-1.1547 StartZ=0 EndX=-2e-16 EndY=-2.3094 EndZ=0
    g3: LineSegment StartX=-2e-16 StartY=-2.3094 StartZ=0 EndX=2 EndY=-1.1547 EndZ=0
    g4: LineSegment StartX=2 StartY=-1.1547 StartZ=0 EndX=2 EndY=1.1547 EndZ=0
    g5: LineSegment StartX=2 StartY=1.1547 StartZ=0 EndX=0 EndY=2.3094 EndZ=0
    g6: Circle [constr] CenterX=0 CenterY=0 CenterZ=0 NormalX=0 NormalY=0 NormalZ=1 AngleXU=0 Radius=2.3094
    g7: Circle CenterX=0 CenterY=0 CenterZ=0 NormalX=0 NormalY=0 NormalZ=1 AngleXU=0 Radius=1
  constraints (18):
    c: Coincident(g0,g1)
    c: Coincident(g1,g2)
    c: Coincident(g2,g3)
    c: Coincident(g3,g4)
    c: Coincident(g4,g5)
    c: Coincident(g5,g0)
    c: Equal(g0, g1-g5) x5
    c: PointOnObject(g0,g6)
    c: PointOnObject(g1,g6)
    c: PointOnObject(g2,g6)
    c: PointOnObject(g3,g6)
    c: PointOnObject(g4,g6)
    c: PointOnObject(g5,g6)
    c: Coincident(g6,g-1)
    c: PointOnObject(g5,g-2)
    c: DistanceX(g0,g4) = 4
    c: Coincident(g7,g-1)
    c: Radius(g7) = 1
FEATURE [PartDesign::Pad] Pad241  label="M3 Nut Primitive043"
  Length = 0.6
  Length2 = 0.6
  Profile = -> Sketch609
  Type = 4
FEATURE [Sketcher::SketchObject] Sketch608
  ExternalGeometry = -> [Pad241]
  MapMode = 5
  Placement = pos=(0,0,0) rot=(0.57735,0.57735,0.57735;2.0944rad)
  Support = -> [YZ_Plane202]
  sketch-geometry (6):
    g0: LineSegment StartX=-1.9594 StartY=0.6 StartZ=0 EndX=-2.8094 EndY=0.6 EndZ=0
    g1: LineSegment StartX=-2.8094 StartY=0.6 StartZ=0 EndX=-2.8094 EndY=-0.6 EndZ=0
    g2: LineSegment StartX=-2.8094 StartY=-0.6 StartZ=0 EndX=-1.9594 EndY=-0.6 EndZ=0
    g3: LineSegment StartX=-1.9594 StartY=-0.6 StartZ=0 EndX=-2.3094 EndY=-0.4 EndZ=0
    g4: LineSegment StartX=-2.3094 StartY=-0.4 StartZ=0 EndX=-2.3094 EndY=0.4 EndZ=0
    g5: LineSegment StartX=-2.3094 StartY=0.4 StartZ=0 EndX=-1.9594 EndY=0.6 EndZ=0
  constraints (15):
    c: Horizontal(g0)
    c: Coincident(g0,g1)
    c: Coincident(g1,g2)
    c: Coincident(g2,g3)
    c: Coincident(g3,g4)
    c: Coincident(g4,g5)
    c: Coincident(g5,g0)
    c: Symmetric(g4,g3,g-1)
    c: Symmetric(g0,g2,g-1)
    c: Symmetric(g1,g0,g-1)
    c: DistanceX(g0,g4) = 0.5
    c: DistanceY(g3,g4) = 0.8
    c: DistanceY(g1,g0) = 1.2
    c: PointOnObject(g3,g-3)
    c: DistanceX(g4,g0) = 0.35
FEATURE [PartDesign::Groove] Groove046  label="M3 Nut Smooth044"
  Angle = 360
  Axis = (-2e-16,3e-16,1)
  Base = (0,0,0)
  BaseFeature = -> Pad241
  Profile = -> Sketch608
  ReferenceAxis = -> Sketch608 [V_Axis]
  Reversed = true
FEATURE [PartDesign::Chamfer] Chamfer098  label="M3 Nut Smooth Hole041"
  Base = -> Groove046 [Edge24,Edge23]
  BaseFeature = -> Groove046
  Size = 0.2
FEATURE [PartDesign::Body] Body148  label="M2 Nut023"
  Group = -> [Sketch609,Pad241,Sketch608,Groove046,Chamfer098,Sketch600,Sketch599]
  Origin = -> Origin209
  Placement = pos=(0,0,2.75) rot=(0,0,1;0rad)
  Tip = -> Chamfer098
FEATURE [Sketcher::SketchObject] Sketch612
  MapMode = 5
  Support = -> [XY_Plane201]
FEATURE [Sketcher::SketchObject] Sketch614
  MapMode = 5
  Placement = pos=(0,0,2) rot=(0,0,1;0rad)
  Support = -> [Pad234]
  sketch-geometry (1):
    g0: Circle CenterX=0 CenterY=0 CenterZ=0 NormalX=0 NormalY=0 NormalZ=1 AngleXU=0 Radius=1
  constraints (2):
    c: Coincident(g0,g-1)
    c: Radius(g0) = 1
FEATURE [PartDesign::Pad] Pad231  label="M3x8 Thread025"
  BaseFeature = -> Pad234
  Length = 8
  Length2 = 100
  Profile = -> Sketch614
  Type = 0
FEATURE [Sketcher::SketchObject] Sketch611
  MapMode = 5
  Placement = pos=(0,0,0) rot=(1,0,0;3.14159rad)
  Support = -> [Pad231]
  sketch-geometry (7):
    g0: LineSegment StartX=0.77 StartY=0.44456 StartZ=0 EndX=0 EndY=0.889119 EndZ=0
    g1: LineSegment StartX=0 StartY=0.889119 StartZ=0 EndX=-0.77 EndY=0.44456 EndZ=0
    g2: LineSegment StartX=-0.77 StartY=0.44456 StartZ=0 EndX=-0.77 EndY=-0.44456 EndZ=0
    g3: LineSegment StartX=-0.77 StartY=-0.44456 StartZ=0 EndX=3.85628e-11 EndY=-0.889119 EndZ=0
    g4: LineSegment StartX=3.85628e-11 StartY=-0.889119 StartZ=0 EndX=0.77 EndY=-0.44456 EndZ=0
    g5: LineSegment StartX=0.77 StartY=-0.44456 StartZ=0 EndX=0.77 EndY=0.44456 EndZ=0
    g6: Circle [constr] CenterX=0 CenterY=0 CenterZ=0 NormalX=0 NormalY=0 NormalZ=1 AngleXU=0 Radius=0.889119
  constraints (16):
    c: Coincident(g0,g1)
    c: Coincident(g1,g2)
    c: Coincident(g2,g3)
    c: Coincident(g3,g4)
    c: Coincident(g4,g5)
    c: Coincident(g5,g0)
    c: Equal(g0, g1-g5) x5
    c: PointOnObject(g0,g6)
    c: PointOnObject(g1,g6)
    c: PointOnObject(g2,g6)
    c: PointOnObject(g3,g6)
    c: PointOnObject(g4,g6)
    c: PointOnObject(g5,g6)
    c: Coincident(g6,g-1)
    c: PointOnObject(g0,g-2)
    c: DistanceX(g1,g0) = 1.54
FEATURE [PartDesign::Pocket] Pocket262  label="M3x8 Wrench028"
  BaseFeature = -> Pad231
  Length = 1
  Length2 = 100
  Profile = -> Sketch611
  Type = 0
FEATURE [PartDesign::Chamfer] Chamfer101  label="M3x8 Smooth027"
  Base = -> Pocket262 [Face11,Edge2,Edge24,Edge3]
  BaseFeature = -> Pocket262
  Size = 0.2
FEATURE [PartDesign::Body] Body146  label="M2x031"
  Group = -> [Sketch601,Pad234,Sketch614,Pad231,Sketch611,Pocket262,Chamfer101]
  Origin = -> Origin188
  Tip = -> Chamfer101
FEATURE [App::Part] Part055  label="M020"
  Group = -> [Body146,Body148]
  Origin = -> Origin217
  Placement = pos=(-9.1,-5.25,80) rot=(0,1,0;3.14159rad)
FEATURE [Sketcher::SketchObject] Sketch617
  MapMode = 5
  Placement = pos=(0,0,2) rot=(0,0,1;0rad)
  Support = -> [Pad233]
  sketch-geometry (1):
    g0: Circle CenterX=0 CenterY=0 CenterZ=0 NormalX=0 NormalY=0 NormalZ=1 AngleXU=0 Radius=1
  constraints (2):
    c: Coincident(g0,g-1)
    c: Radius(g0) = 1
FEATURE [PartDesign::Pad] Pad232  label="M3x8 Thread026"
  BaseFeature = -> Pad233
  Length = 8
  Length2 = 100
  Profile = -> Sketch617
  Type = 0
FEATURE [Sketcher::SketchObject] Sketch613
  MapMode = 5
  Placement = pos=(0,0,0) rot=(1,0,0;3.14159rad)
  Support = -> [Pad232]
  sketch-geometry (7):
    g0: LineSegment StartX=0.77 StartY=0.44456 StartZ=0 EndX=0 EndY=0.889119 EndZ=0
    g1: LineSegment StartX=0 StartY=0.889119 StartZ=0 EndX=-0.77 EndY=0.44456 EndZ=0
    g2: LineSegment StartX=-0.77 StartY=0.44456 StartZ=0 EndX=-0.77 EndY=-0.44456 EndZ=0
    g3: LineSegment StartX=-0.77 StartY=-0.44456 StartZ=0 EndX=3.85628e-11 EndY=-0.889119 EndZ=0
    g4: LineSegment StartX=3.85628e-11 StartY=-0.889119 StartZ=0 EndX=0.77 EndY=-0.44456 EndZ=0
    g5: LineSegment StartX=0.77 StartY=-0.44456 StartZ=0 EndX=0.77 EndY=0.44456 EndZ=0
    g6: Circle [constr] CenterX=0 CenterY=0 CenterZ=0 NormalX=0 NormalY=0 NormalZ=1 AngleXU=0 Radius=0.889119
  constraints (16):
    c: Coincident(g0,g1)
    c: Coincident(g1,g2)
    c: Coincident(g2,g3)
    c: Coincident(g3,g4)
    c: Coincident(g4,g5)
    c: Coincident(g5,g0)
    c: Equal(g0, g1-g5) x5
    c: PointOnObject(g0,g6)
    c: PointOnObject(g1,g6)
    c: PointOnObject(g2,g6)
    c: PointOnObject(g3,g6)
    c: PointOnObject(g4,g6)
    c: PointOnObject(g5,g6)
    c: Coincident(g6,g-1)
    c: PointOnObject(g0,g-2)
    c: DistanceX(g1,g0) = 1.54
FEATURE [PartDesign::Pocket] Pocket259  label="M3x8 Wrench026"
  BaseFeature = -> Pad232
  Length = 1
  Length2 = 100
  Profile = -> Sketch613
  Type = 0
FEATURE [PartDesign::Chamfer] Chamfer099  label="M3x8 Smooth025"
  Base = -> Pocket259 [Face11,Edge2,Edge24,Edge3]
  BaseFeature = -> Pocket259
  Size = 0.2
FEATURE [PartDesign::Body] Body151  label="M2x033"
  Group = -> [Sketch604,Pad233,Sketch617,Pad232,Sketch613,Pocket259,Chamfer099]
  Origin = -> Origin218
  Tip = -> Chamfer099
FEATURE [Sketcher::SketchObject] Sketch618
  MapMode = 5
  Support = -> [XY_Plane201]
  sketch-geometry (8):
    g0: LineSegment StartX=0 StartY=2.3094 StartZ=0 EndX=-2 EndY=1.1547 EndZ=0
    g1: LineSegment StartX=-2 StartY=1.1547 StartZ=0 EndX=-2 EndY=-1.1547 EndZ=0
    g2: LineSegment StartX=-2 StartY=-1.1547 StartZ=0 EndX=-2e-16 EndY=-2.3094 EndZ=0
    g3: LineSegment StartX=-2e-16 StartY=-2.3094 StartZ=0 EndX=2 EndY=-1.1547 EndZ=0
    g4: LineSegment StartX=2 StartY=-1.1547 StartZ=0 EndX=2 EndY=1.1547 EndZ=0
    g5: LineSegment StartX=2 StartY=1.1547 StartZ=0 EndX=0 EndY=2.3094 EndZ=0
    g6: Circle [constr] CenterX=0 CenterY=0 CenterZ=0 NormalX=0 NormalY=0 NormalZ=1 AngleXU=0 Radius=2.3094
    g7: Circle CenterX=0 CenterY=0 CenterZ=0 NormalX=0 NormalY=0 NormalZ=1 AngleXU=0 Radius=1
  constraints (18):
    c: Coincident(g0,g1)
    c: Coincident(g1,g2)
    c: Coincident(g2,g3)
    c: Coincident(g3,g4)
    c: Coincident(g4,g5)
    c: Coincident(g5,g0)
    c: Equal(g0, g1-g5) x5
    c: PointOnObject(g0,g6)
    c: PointOnObject(g1,g6)
    c: PointOnObject(g2,g6)
    c: PointOnObject(g3,g6)
    c: PointOnObject(g4,g6)
    c: PointOnObject(g5,g6)
    c: Coincident(g6,g-1)
    c: PointOnObject(g5,g-2)
    c: DistanceX(g0,g4) = 4
    c: Coincident(g7,g-1)
    c: Radius(g7) = 1
FEATURE [PartDesign::Pad] Pad235  label="M3 Nut Primitive041"
  Length = 0.6
  Length2 = 0.6
  Profile = -> Sketch618
  Type = 4
FEATURE [Sketcher::SketchObject] Sketch575
  ExternalGeometry = -> [Pad235]
  MapMode = 5
  Placement = pos=(0,0,0) rot=(0.57735,0.57735,0.57735;2.0944rad)
  Support = -> [YZ_Plane198]
  sketch-geometry (6):
    g0: LineSegment StartX=-1.9594 StartY=0.6 StartZ=0 EndX=-2.8094 EndY=0.6 EndZ=0
    g1: LineSegment StartX=-2.8094 StartY=0.6 StartZ=0 EndX=-2.8094 EndY=-0.6 EndZ=0
    g2: LineSegment StartX=-2.8094 StartY=-0.6 StartZ=0 EndX=-1.9594 EndY=-0.6 EndZ=0
    g3: LineSegment StartX=-1.9594 StartY=-0.6 StartZ=0 EndX=-2.3094 EndY=-0.4 EndZ=0
    g4: LineSegment StartX=-2.3094 StartY=-0.4 StartZ=0 EndX=-2.3094 EndY=0.4 EndZ=0
    g5: LineSegment StartX=-2.3094 StartY=0.4 StartZ=0 EndX=-1.9594 EndY=0.6 EndZ=0
  constraints (15):
    c: Horizontal(g0)
    c: Coincident(g0,g1)
    c: Coincident(g1,g2)
    c: Coincident(g2,g3)
    c: Coincident(g3,g4)
    c: Coincident(g4,g5)
    c: Coincident(g5,g0)
    c: Symmetric(g4,g3,g-1)
    c: Symmetric(g0,g2,g-1)
    c: Symmetric(g1,g0,g-1)
    c: DistanceX(g0,g4) = 0.5
    c: DistanceY(g3,g4) = 0.8
    c: DistanceY(g1,g0) = 1.2
    c: PointOnObject(g3,g-3)
    c: DistanceX(g4,g0) = 0.35
FEATURE [PartDesign::Groove] Groove043  label="M3 Nut Smooth041"
  Angle = 360
  Axis = (-2e-16,3e-16,1)
  Base = (0,0,0)
  BaseFeature = -> Pad235
  Profile = -> Sketch575
  ReferenceAxis = -> Sketch575 [V_Axis]
  Reversed = true
FEATURE [PartDesign::Chamfer] Chamfer107  label="M3 Nut Smooth Hole046"
  Base = -> Groove043 [Edge24,Edge23]
  BaseFeature = -> Groove043
  Size = 0.2
FEATURE [PartDesign::Body] Body142  label="M2 Nut021"
  Group = -> [Sketch618,Pad235,Sketch575,Groove043,Chamfer107,Sketch607,Sketch612]
  Origin = -> Origin192
  Placement = pos=(0,0,2.75) rot=(0,0,1;0rad)
  Tip = -> Chamfer107
FEATURE [App::Part] Part057  label="M021"
  Group = -> [Body151,Body142]
  Origin = -> Origin195
  Placement = pos=(-9.8e-15,-10.5,80) rot=(0,1,0;3.14159rad)
FEATURE [Sketcher::SketchObject] Sketch620
  MapMode = 5
  Support = -> [XY_Plane214]
FEATURE [Sketcher::SketchObject] Sketch621
  MapMode = 5
  Support = -> [XY_Plane214]
FEATURE [Sketcher::SketchObject] Sketch622
  ExternalGeometry = -> [Pad242]
  MapMode = 5
  Placement = pos=(0,0,0) rot=(0.57735,0.57735,0.57735;2.0944rad)
  Support = -> [YZ_Plane208]
  sketch-geometry (6):
    g0: LineSegment StartX=-1.9594 StartY=0.6 StartZ=0 EndX=-2.8094 EndY=0.6 EndZ=0
    g1: LineSegment StartX=-2.8094 StartY=0.6 StartZ=0 EndX=-2.8094 EndY=-0.6 EndZ=0
    g2: LineSegment StartX=-2.8094 StartY=-0.6 StartZ=0 EndX=-1.9594 EndY=-0.6 EndZ=0
    g3: LineSegment StartX=-1.9594 StartY=-0.6 StartZ=0 EndX=-2.3094 EndY=-0.4 EndZ=0
    g4: LineSegment StartX=-2.3094 StartY=-0.4 StartZ=0 EndX=-2.3094 EndY=0.4 EndZ=0
    g5: LineSegment StartX=-2.3094 StartY=0.4 StartZ=0 EndX=-1.9594 EndY=0.6 EndZ=0
  constraints (15):
    c: Horizontal(g0)
    c: Coincident(g0,g1)
    c: Coincident(g1,g2)
    c: Coincident(g2,g3)
    c: Coincident(g3,g4)
    c: Coincident(g4,g5)
    c: Coincident(g5,g0)
    c: Symmetric(g4,g3,g-1)
    c: Symmetric(g0,g2,g-1)
    c: Symmetric(g1,g0,g-1)
    c: DistanceX(g0,g4) = 0.5
    c: DistanceY(g3,g4) = 0.8
    c: DistanceY(g1,g0) = 1.2
    c: PointOnObject(g3,g-3)
    c: DistanceX(g4,g0) = 0.35
FEATURE [PartDesign::Groove] Groove047  label="M3 Nut Smooth045"
  Angle = 360
  Axis = (-2e-16,3e-16,1)
  Base = (0,0,0)
  BaseFeature = -> Pad242
  Profile = -> Sketch622
  ReferenceAxis = -> Sketch622 [V_Axis]
  Reversed = true
FEATURE [PartDesign::Chamfer] Chamfer109  label="M3 Nut Smooth Hole047"
  Base = -> Groove047 [Edge24,Edge23]
  BaseFeature = -> Groove047
  Size = 0.2
FEATURE [PartDesign::Body] Body145  label="M2 Nut022"
  Group = -> [Sketch576,Pad242,Sketch622,Groove047,Chamfer109,Sketch620,Sketch621]
  Origin = -> Origin183
  Placement = pos=(0,0,2.75) rot=(0,0,1;0rad)
  Tip = -> Chamfer109
FEATURE [Sketcher::SketchObject] Sketch624
  MapMode = 5
  Support = -> [XY_Plane212]
  sketch-geometry (1):
    g0: Circle CenterX=0 CenterY=0 CenterZ=0 NormalX=0 NormalY=0 NormalZ=1 AngleXU=0 Radius=1.9
  constraints (2):
    c: Coincident(g0,g-1)
    c: Radius(g0) = 1.9
FEATURE [PartDesign::Pad] Pad243  label="M3x8 Head028"
  Length = 2
  Length2 = 100
  Profile = -> Sketch624
  Type = 0
FEATURE [Sketcher::SketchObject] Sketch616
  MapMode = 5
  Placement = pos=(0,0,2) rot=(0,0,1;0rad)
  Support = -> [Pad243]
  sketch-geometry (1):
    g0: Circle CenterX=0 CenterY=0 CenterZ=0 NormalX=0 NormalY=0 NormalZ=1 AngleXU=0 Radius=1
  constraints (2):
    c: Coincident(g0,g-1)
    c: Radius(g0) = 1
FEATURE [PartDesign::Pad] Pad248  label="M3x8 Thread030"
  BaseFeature = -> Pad243
  Length = 8
  Length2 = 100
  Profile = -> Sketch616
  Type = 0
FEATURE [Sketcher::SketchObject] Sketch623
  MapMode = 5
  Placement = pos=(0,0,0) rot=(1,0,0;3.14159rad)
  Support = -> [Pad248]
  sketch-geometry (7):
    g0: LineSegment StartX=0.77 StartY=0.44456 StartZ=0 EndX=0 EndY=0.889119 EndZ=0
    g1: LineSegment StartX=0 StartY=0.889119 StartZ=0 EndX=-0.77 EndY=0.44456 EndZ=0
    g2: LineSegment StartX=-0.77 StartY=0.44456 StartZ=0 EndX=-0.77 EndY=-0.44456 EndZ=0
    g3: LineSegment StartX=-0.77 StartY=-0.44456 StartZ=0 EndX=3.85628e-11 EndY=-0.889119 EndZ=0
    g4: LineSegment StartX=3.85628e-11 StartY=-0.889119 StartZ=0 EndX=0.77 EndY=-0.44456 EndZ=0
    g5: LineSegment StartX=0.77 StartY=-0.44456 StartZ=0 EndX=0.77 EndY=0.44456 EndZ=0
    g6: Circle [constr] CenterX=0 CenterY=0 CenterZ=0 NormalX=0 NormalY=0 NormalZ=1 AngleXU=0 Radius=0.889119
  constraints (16):
    c: Coincident(g0,g1)
    c: Coincident(g1,g2)
    c: Coincident(g2,g3)
    c: Coincident(g3,g4)
    c: Coincident(g4,g5)
    c: Coincident(g5,g0)
    c: Equal(g0, g1-g5) x5
    c: PointOnObject(g0,g6)
    c: PointOnObject(g1,g6)
    c: PointOnObject(g2,g6)
    c: PointOnObject(g3,g6)
    c: PointOnObject(g4,g6)
    c: PointOnObject(g5,g6)
    c: Coincident(g6,g-1)
    c: PointOnObject(g0,g-2)
    c: DistanceX(g1,g0) = 1.54
FEATURE [PartDesign::Pocket] Pocket263  label="M3x8 Wrench029"
  BaseFeature = -> Pad248
  Length = 1
  Length2 = 100
  Profile = -> Sketch623
  Type = 0
FEATURE [PartDesign::Chamfer] Chamfer111  label="M3x8 Smooth030"
  Base = -> Pocket263 [Face11,Edge2,Edge24,Edge3]
  BaseFeature = -> Pocket263
  Size = 0.2
FEATURE [PartDesign::Body] Body141  label="M2x029"
  Group = -> [Sketch624,Pad243,Sketch616,Pad248,Sketch623,Pocket263,Chamfer111]
  Origin = -> Origin199
  Tip = -> Chamfer111
FEATURE [Sketcher::SketchObject] Sketch626
  MapMode = 5
  Support = -> [XY_Plane210]
  sketch-geometry (8):
    g0: LineSegment StartX=0 StartY=2.3094 StartZ=0 EndX=-2 EndY=1.1547 EndZ=0
    g1: LineSegment StartX=-2 StartY=1.1547 StartZ=0 EndX=-2 EndY=-1.1547 EndZ=0
    g2: LineSegment StartX=-2 StartY=-1.1547 StartZ=0 EndX=-2e-16 EndY=-2.3094 EndZ=0
    g3: LineSegment StartX=-2e-16 StartY=-2.3094 StartZ=0 EndX=2 EndY=-1.1547 EndZ=0
    g4: LineSegment StartX=2 StartY=-1.1547 StartZ=0 EndX=2 EndY=1.1547 EndZ=0
    g5: LineSegment StartX=2 StartY=1.1547 StartZ=0 EndX=0 EndY=2.3094 EndZ=0
    g6: Circle [constr] CenterX=0 CenterY=0 CenterZ=0 NormalX=0 NormalY=0 NormalZ=1 AngleXU=0 Radius=2.3094
    g7: Circle CenterX=0 CenterY=0 CenterZ=0 NormalX=0 NormalY=0 NormalZ=1 AngleXU=0 Radius=1
  constraints (18):
    c: Coincident(g0,g1)
    c: Coincident(g1,g2)
    c: Coincident(g2,g3)
    c: Coincident(g3,g4)
    c: Coincident(g4,g5)
    c: Coincident(g5,g0)
    c: Equal(g0, g1-g5) x5
    c: PointOnObject(g0,g6)
    c: PointOnObject(g1,g6)
    c: PointOnObject(g2,g6)
    c: PointOnObject(g3,g6)
    c: PointOnObject(g4,g6)
    c: PointOnObject(g5,g6)
    c: Coincident(g6,g-1)
    c: PointOnObject(g5,g-2)
    c: DistanceX(g0,g4) = 4
    c: Coincident(g7,g-1)
    c: Radius(g7) = 1
FEATURE [PartDesign::Pad] Pad244  label="M3 Nut Primitive045"
  Length = 0.6
  Length2 = 0.6
  Profile = -> Sketch626
  Type = 4
FEATURE [Sketcher::SketchObject] Sketch619
  ExternalGeometry = -> [Pad244]
  MapMode = 5
  Placement = pos=(0,0,0) rot=(0.57735,0.57735,0.57735;2.0944rad)
  Support = -> [YZ_Plane207]
  sketch-geometry (6):
    g0: LineSegment StartX=-1.9594 StartY=0.6 StartZ=0 EndX=-2.8094 EndY=0.6 EndZ=0
    g1: LineSegment StartX=-2.8094 StartY=0.6 StartZ=0 EndX=-2.8094 EndY=-0.6 EndZ=0
    g2: LineSegment StartX=-2.8094 StartY=-0.6 StartZ=0 EndX=-1.9594 EndY=-0.6 EndZ=0
    g3: LineSegment StartX=-1.9594 StartY=-0.6 StartZ=0 EndX=-2.3094 EndY=-0.4 EndZ=0
    g4: LineSegment StartX=-2.3094 StartY=-0.4 StartZ=0 EndX=-2.3094 EndY=0.4 EndZ=0
    g5: LineSegment StartX=-2.3094 StartY=0.4 StartZ=0 EndX=-1.9594 EndY=0.6 EndZ=0
  constraints (15):
    c: Horizontal(g0)
    c: Coincident(g0,g1)
    c: Coincident(g1,g2)
    c: Coincident(g2,g3)
    c: Coincident(g3,g4)
    c: Coincident(g4,g5)
    c: Coincident(g5,g0)
    c: Symmetric(g4,g3,g-1)
    c: Symmetric(g0,g2,g-1)
    c: Symmetric(g1,g0,g-1)
    c: DistanceX(g0,g4) = 0.5
    c: DistanceY(g3,g4) = 0.8
    c: DistanceY(g1,g0) = 1.2
    c: PointOnObject(g3,g-3)
    c: DistanceX(g4,g0) = 0.35
FEATURE [PartDesign::Groove] Groove048  label="M3 Nut Smooth046"
  Angle = 360
  Axis = (-2e-16,3e-16,1)
  Base = (0,0,0)
  BaseFeature = -> Pad244
  Profile = -> Sketch619
  ReferenceAxis = -> Sketch619 [V_Axis]
  Reversed = true
FEATURE [PartDesign::Chamfer] Chamfer106  label="M3 Nut Smooth Hole045"
  Base = -> Groove048 [Edge24,Edge23]
  BaseFeature = -> Groove048
  Size = 0.2
FEATURE [Sketcher::SketchObject] Sketch627
  MapMode = 5
  Support = -> [XY_Plane200]
  sketch-geometry (8):
    g0: LineSegment StartX=0 StartY=2.3094 StartZ=0 EndX=-2 EndY=1.1547 EndZ=0
    g1: LineSegment StartX=-2 StartY=1.1547 StartZ=0 EndX=-2 EndY=-1.1547 EndZ=0
    g2: LineSegment StartX=-2 StartY=-1.1547 StartZ=0 EndX=-2e-16 EndY=-2.3094 EndZ=0
    g3: LineSegment StartX=-2e-16 StartY=-2.3094 StartZ=0 EndX=2 EndY=-1.1547 EndZ=0
    g4: LineSegment StartX=2 StartY=-1.1547 StartZ=0 EndX=2 EndY=1.1547 EndZ=0
    g5: LineSegment StartX=2 StartY=1.1547 StartZ=0 EndX=0 EndY=2.3094 EndZ=0
    g6: Circle [constr] CenterX=0 CenterY=0 CenterZ=0 NormalX=0 NormalY=0 NormalZ=1 AngleXU=0 Radius=2.3094
    g7: Circle CenterX=0 CenterY=0 CenterZ=0 NormalX=0 NormalY=0 NormalZ=1 AngleXU=0 Radius=1
  constraints (18):
    c: Coincident(g0,g1)
    c: Coincident(g1,g2)
    c: Coincident(g2,g3)
    c: Coincident(g3,g4)
    c: Coincident(g4,g5)
    c: Coincident(g5,g0)
    c: Equal(g0, g1-g5) x5
    c: PointOnObject(g0,g6)
    c: PointOnObject(g1,g6)
    c: PointOnObject(g2,g6)
    c: PointOnObject(g3,g6)
    c: PointOnObject(g4,g6)
    c: PointOnObject(g5,g6)
    c: Coincident(g6,g-1)
    c: PointOnObject(g5,g-2)
    c: DistanceX(g0,g4) = 4
    c: Coincident(g7,g-1)
    c: Radius(g7) = 1
FEATURE [PartDesign::Pad] Pad250  label="M3 Nut Primitive046"
  Length = 0.6
  Length2 = 0.6
  Profile = -> Sketch627
  Type = 4
FEATURE [Sketcher::SketchObject] Sketch629
  MapMode = 5
  Support = -> [XY_Plane207]
  sketch-geometry (1):
    g0: Circle CenterX=0 CenterY=0 CenterZ=0 NormalX=0 NormalY=0 NormalZ=1 AngleXU=0 Radius=1.9
  constraints (2):
    c: Coincident(g0,g-1)
    c: Radius(g0) = 1.9
FEATURE [PartDesign::Pad] Pad249  label="M3x8 Head030"
  Length = 2
  Length2 = 100
  Profile = -> Sketch629
  Type = 0
FEATURE [Sketcher::SketchObject] Sketch610
  MapMode = 5
  Placement = pos=(0,0,2) rot=(0,0,1;0rad)
  Support = -> [Pad249]
  sketch-geometry (1):
    g0: Circle CenterX=0 CenterY=0 CenterZ=0 NormalX=0 NormalY=0 NormalZ=1 AngleXU=0 Radius=1
  constraints (2):
    c: Coincident(g0,g-1)
    c: Radius(g0) = 1
FEATURE [PartDesign::Pad] Pad240  label="M3x8 Thread027"
  BaseFeature = -> Pad249
  Length = 8
  Length2 = 100
  Profile = -> Sketch610
  Type = 0
FEATURE [Sketcher::SketchObject] Sketch615
  MapMode = 5
  Placement = pos=(0,0,0) rot=(1,0,0;3.14159rad)
  Support = -> [Pad240]
  sketch-geometry (7):
    g0: LineSegment StartX=0.77 StartY=0.44456 StartZ=0 EndX=0 EndY=0.889119 EndZ=0
    g1: LineSegment StartX=0 StartY=0.889119 StartZ=0 EndX=-0.77 EndY=0.44456 EndZ=0
    g2: LineSegment StartX=-0.77 StartY=0.44456 StartZ=0 EndX=-0.77 EndY=-0.44456 EndZ=0
    g3: LineSegment StartX=-0.77 StartY=-0.44456 StartZ=0 EndX=3.85628e-11 EndY=-0.889119 EndZ=0
    g4: LineSegment StartX=3.85628e-11 StartY=-0.889119 StartZ=0 EndX=0.77 EndY=-0.44456 EndZ=0
    g5: LineSegment StartX=0.77 StartY=-0.44456 StartZ=0 EndX=0.77 EndY=0.44456 EndZ=0
    g6: Circle [constr] CenterX=0 CenterY=0 CenterZ=0 NormalX=0 NormalY=0 NormalZ=1 AngleXU=0 Radius=0.889119
  constraints (16):
    c: Coincident(g0,g1)
    c: Coincident(g1,g2)
    c: Coincident(g2,g3)
    c: Coincident(g3,g4)
    c: Coincident(g4,g5)
    c: Coincident(g5,g0)
    c: Equal(g0, g1-g5) x5
    c: PointOnObject(g0,g6)
    c: PointOnObject(g1,g6)
    c: PointOnObject(g2,g6)
    c: PointOnObject(g3,g6)
    c: PointOnObject(g4,g6)
    c: PointOnObject(g5,g6)
    c: Coincident(g6,g-1)
    c: PointOnObject(g0,g-2)
    c: DistanceX(g1,g0) = 1.54
FEATURE [PartDesign::Pocket] Pocket264  label="M3x8 Wrench030"
  BaseFeature = -> Pad240
  Length = 1
  Length2 = 100
  Profile = -> Sketch615
  Type = 0
FEATURE [PartDesign::Chamfer] Chamfer102  label="M3x8 Smooth028"
  Base = -> Pocket264 [Face11,Edge2,Edge24,Edge3]
  BaseFeature = -> Pocket264
  Size = 0.2
FEATURE [PartDesign::Body] Body147  label="M2x032"
  Group = -> [Sketch629,Pad249,Sketch610,Pad240,Sketch615,Pocket264,Chamfer102]
  Origin = -> Origin200
  Tip = -> Chamfer102
FEATURE [App::Part] Part060  label="M023"
  Group = -> [Body147,Body145]
  Origin = -> Origin193
  Placement = pos=(9.1,-5.25,80) rot=(0,1,0;3.14159rad)
FEATURE [Sketcher::SketchObject] Sketch630
  MapMode = 5
  Support = -> [XY_Plane200]
FEATURE [Sketcher::SketchObject] Sketch632
  MapMode = 5
  Support = -> [XY_Plane210]
FEATURE [Sketcher::SketchObject] Sketch633
  ExternalGeometry = -> [Pad250]
  MapMode = 5
  Placement = pos=(0,0,0) rot=(0.57735,0.57735,0.57735;2.0944rad)
  Support = -> [YZ_Plane199]
  sketch-geometry (6):
    g0: LineSegment StartX=-1.9594 StartY=0.6 StartZ=0 EndX=-2.8094 EndY=0.6 EndZ=0
    g1: LineSegment StartX=-2.8094 StartY=0.6 StartZ=0 EndX=-2.8094 EndY=-0.6 EndZ=0
    g2: LineSegment StartX=-2.8094 StartY=-0.6 StartZ=0 EndX=-1.9594 EndY=-0.6 EndZ=0
    g3: LineSegment StartX=-1.9594 StartY=-0.6 StartZ=0 EndX=-2.3094 EndY=-0.4 EndZ=0
    g4: LineSegment StartX=-2.3094 StartY=-0.4 StartZ=0 EndX=-2.3094 EndY=0.4 EndZ=0
    g5: LineSegment StartX=-2.3094 StartY=0.4 StartZ=0 EndX=-1.9594 EndY=0.6 EndZ=0
  constraints (15):
    c: Horizontal(g0)
    c: Coincident(g0,g1)
    c: Coincident(g1,g2)
    c: Coincident(g2,g3)
    c: Coincident(g3,g4)
    c: Coincident(g4,g5)
    c: Coincident(g5,g0)
    c: Symmetric(g4,g3,g-1)
    c: Symmetric(g0,g2,g-1)
    c: Symmetric(g1,g0,g-1)
    c: DistanceX(g0,g4) = 0.5
    c: DistanceY(g3,g4) = 0.8
    c: DistanceY(g1,g0) = 1.2
    c: PointOnObject(g3,g-3)
    c: DistanceX(g4,g0) = 0.35
FEATURE [PartDesign::Groove] Groove045  label="M3 Nut Smooth043"
  Angle = 360
  Axis = (-2e-16,3e-16,1)
  Base = (0,0,0)
  BaseFeature = -> Pad250
  Profile = -> Sketch633
  ReferenceAxis = -> Sketch633 [V_Axis]
  Reversed = true
FEATURE [PartDesign::Chamfer] Chamfer104  label="M3 Nut Smooth Hole043"
  Base = -> Groove045 [Edge24,Edge23]
  BaseFeature = -> Groove045
  Size = 0.2
FEATURE [Sketcher::SketchObject] Sketch634
  MapMode = 5
  Support = -> [XY_Plane210]
FEATURE [PartDesign::Body] Body152  label="M2 Nut025"
  Group = -> [Sketch626,Pad244,Sketch619,Groove048,Chamfer106,Sketch634,Sketch632]
  Origin = -> Origin208
  Placement = pos=(0,0,2.75) rot=(0,0,1;0rad)
  Tip = -> Chamfer106
FEATURE [App::Part] Part061  label="M024"
  Group = -> [Body141,Body152]
  Origin = -> Origin189
  Placement = pos=(9.1,5.25,80) rot=(0,1,0;3.14159rad)
FEATURE [Sketcher::SketchObject] Sketch635
  MapMode = 5
  Support = -> [XY_Plane200]
FEATURE [PartDesign::Body] Body149  label="M2 Nut024"
  Group = -> [Sketch627,Pad250,Sketch633,Groove045,Chamfer104,Sketch635,Sketch630]
  Origin = -> Origin212
  Placement = pos=(0,0,2.75) rot=(0,0,1;0rad)
  Tip = -> Chamfer104
FEATURE [Sketcher::SketchObject] Sketch636
  MapMode = 5
  Support = -> [XY_Plane208]
  sketch-geometry (1):
    g0: Circle CenterX=0 CenterY=0 CenterZ=0 NormalX=0 NormalY=0 NormalZ=1 AngleXU=0 Radius=1.9
  constraints (2):
    c: Coincident(g0,g-1)
    c: Radius(g0) = 1.9
FEATURE [PartDesign::Pad] Pad247  label="M3x8 Head029"
  Length = 2
  Length2 = 100
  Profile = -> Sketch636
  Type = 0
FEATURE [Sketcher::SketchObject] Sketch637
  MapMode = 5
  Support = -> [XY_Plane188]
  sketch-geometry (8):
    g0: LineSegment StartX=0 StartY=3.17543 StartZ=0 EndX=-2.75 EndY=1.58771 EndZ=0
    g1: LineSegment StartX=-2.75 StartY=1.58771 StartZ=0 EndX=-2.75 EndY=-1.58771 EndZ=0
    g2: LineSegment StartX=-2.75 StartY=-1.58771 StartZ=0 EndX=0 EndY=-3.17543 EndZ=0
    g3: LineSegment StartX=0 StartY=-3.17543 StartZ=0 EndX=2.75 EndY=-1.58771 EndZ=0
    g4: LineSegment StartX=2.75 StartY=-1.58771 StartZ=0 EndX=2.75 EndY=1.58771 EndZ=0
    g5: LineSegment StartX=2.75 StartY=1.58771 StartZ=0 EndX=0 EndY=3.17543 EndZ=0
    g6: Circle [constr] CenterX=0 CenterY=0 CenterZ=0 NormalX=0 NormalY=0 NormalZ=1 AngleXU=0 Radius=3.17543
    g7: Circle CenterX=0 CenterY=0 CenterZ=0 NormalX=0 NormalY=0 NormalZ=1 AngleXU=0 Radius=1.5
  constraints (18):
    c: Coincident(g0,g1)
    c: Coincident(g1,g2)
    c: Coincident(g2,g3)
    c: Coincident(g3,g4)
    c: Coincident(g4,g5)
    c: Coincident(g5,g0)
    c: Equal(g0, g1-g5) x5
    c: PointOnObject(g0,g6)
    c: PointOnObject(g1,g6)
    c: PointOnObject(g2,g6)
    c: PointOnObject(g3,g6)
    c: PointOnObject(g4,g6)
    c: PointOnObject(g5,g6)
    c: Coincident(g6,g-1)
    c: PointOnObject(g5,g-2)
    c: DistanceX(g0,g4) = 5.5
    c: Coincident(g7,g-1)
    c: Radius(g7) = 1.5
FEATURE [PartDesign::Pad] Pad255  label="M3 Nut Primitive047"
  Length = 1.2
  Length2 = 1.2
  Profile = -> Sketch637
  Type = 4
FEATURE [Sketcher::SketchObject] Sketch638
  MapMode = 5
  Support = -> [XY_Plane193]
  sketch-geometry (1):
    g0: Circle CenterX=0 CenterY=0 CenterZ=0 NormalX=0 NormalY=0 NormalZ=1 AngleXU=0 Radius=2.75
  constraints (2):
    c: Coincident(g0,g-1)
    c: Radius(g0) = 2.75
FEATURE [PartDesign::Pad] Pad253  label="M3x8 Head032"
  Length = 3
  Length2 = 100
  Profile = -> Sketch638
  Type = 0
FEATURE [Sketcher::SketchObject] Sketch639
  MapMode = 5
  Placement = pos=(0,0,2) rot=(0,0,1;0rad)
  Support = -> [Pad247]
  sketch-geometry (1):
    g0: Circle CenterX=0 CenterY=0 CenterZ=0 NormalX=0 NormalY=0 NormalZ=1 AngleXU=0 Radius=1
  constraints (2):
    c: Coincident(g0,g-1)
    c: Radius(g0) = 1
FEATURE [PartDesign::Pad] Pad245  label="M3x8 Thread028"
  BaseFeature = -> Pad247
  Length = 8
  Length2 = 100
  Profile = -> Sketch639
  Type = 0
FEATURE [Sketcher::SketchObject] Sketch625
  MapMode = 5
  Placement = pos=(0,0,0) rot=(1,0,0;3.14159rad)
  Support = -> [Pad245]
  sketch-geometry (7):
    g0: LineSegment StartX=0.77 StartY=0.44456 StartZ=0 EndX=0 EndY=0.889119 EndZ=0
    g1: LineSegment StartX=0 StartY=0.889119 StartZ=0 EndX=-0.77 EndY=0.44456 EndZ=0
    g2: LineSegment StartX=-0.77 StartY=0.44456 StartZ=0 EndX=-0.77 EndY=-0.44456 EndZ=0
    g3: LineSegment StartX=-0.77 StartY=-0.44456 StartZ=0 EndX=3.85628e-11 EndY=-0.889119 EndZ=0
    g4: LineSegment StartX=3.85628e-11 StartY=-0.889119 StartZ=0 EndX=0.77 EndY=-0.44456 EndZ=0
    g5: LineSegment StartX=0.77 StartY=-0.44456 StartZ=0 EndX=0.77 EndY=0.44456 EndZ=0
    g6: Circle [constr] CenterX=0 CenterY=0 CenterZ=0 NormalX=0 NormalY=0 NormalZ=1 AngleXU=0 Radius=0.889119
  constraints (16):
    c: Coincident(g0,g1)
    c: Coincident(g1,g2)
    c: Coincident(g2,g3)
    c: Coincident(g3,g4)
    c: Coincident(g4,g5)
    c: Coincident(g5,g0)
    c: Equal(g0, g1-g5) x5
    c: PointOnObject(g0,g6)
    c: PointOnObject(g1,g6)
    c: PointOnObject(g2,g6)
    c: PointOnObject(g3,g6)
    c: PointOnObject(g4,g6)
    c: PointOnObject(g5,g6)
    c: Coincident(g6,g-1)
    c: PointOnObject(g0,g-2)
    c: DistanceX(g1,g0) = 1.54
FEATURE [PartDesign::Pocket] Pocket261  label="M3x8 Wrench027"
  BaseFeature = -> Pad245
  Length = 1
  Length2 = 100
  Profile = -> Sketch625
  Type = 0
FEATURE [PartDesign::Chamfer] Chamfer100  label="M3x8 Smooth026"
  Base = -> Pocket261 [Face11,Edge2,Edge24,Edge3]
  BaseFeature = -> Pocket261
  Size = 0.2
FEATURE [PartDesign::Body] Body138  label="M2x027"
  Group = -> [Sketch636,Pad247,Sketch639,Pad245,Sketch625,Pocket261,Chamfer100]
  Origin = -> Origin201
  Tip = -> Chamfer100
FEATURE [App::Part] Part062  label="M025"
  Group = -> [Body138,Body149]
  Origin = -> Origin213
  Placement = pos=(-9.1,5.25,80) rot=(0,1,0;3.14159rad)
FEATURE [Sketcher::SketchObject] Sketch640
  MapMode = 5
  Support = -> [XY_Plane189]
  sketch-geometry (8):
    g0: LineSegment StartX=0 StartY=3.17543 StartZ=0 EndX=-2.75 EndY=1.58771 EndZ=0
    g1: LineSegment StartX=-2.75 StartY=1.58771 StartZ=0 EndX=-2.75 EndY=-1.58771 EndZ=0
    g2: LineSegment StartX=-2.75 StartY=-1.58771 StartZ=0 EndX=0 EndY=-3.17543 EndZ=0
    g3: LineSegment StartX=0 StartY=-3.17543 StartZ=0 EndX=2.75 EndY=-1.58771 EndZ=0
    g4: LineSegment StartX=2.75 StartY=-1.58771 StartZ=0 EndX=2.75 EndY=1.58771 EndZ=0
    g5: LineSegment StartX=2.75 StartY=1.58771 StartZ=0 EndX=0 EndY=3.17543 EndZ=0
    g6: Circle [constr] CenterX=0 CenterY=0 CenterZ=0 NormalX=0 NormalY=0 NormalZ=1 AngleXU=0 Radius=3.17543
    g7: Circle CenterX=0 CenterY=0 CenterZ=0 NormalX=0 NormalY=0 NormalZ=1 AngleXU=0 Radius=1.5
  constraints (18):
    c: Coincident(g0,g1)
    c: Coincident(g1,g2)
    c: Coincident(g2,g3)
    c: Coincident(g3,g4)
    c: Coincident(g4,g5)
    c: Coincident(g5,g0)
    c: Equal(g0, g1-g5) x5
    c: PointOnObject(g0,g6)
    c: PointOnObject(g1,g6)
    c: PointOnObject(g2,g6)
    c: PointOnObject(g3,g6)
    c: PointOnObject(g4,g6)
    c: PointOnObject(g5,g6)
    c: Coincident(g6,g-1)
    c: PointOnObject(g5,g-2)
    c: DistanceX(g0,g4) = 5.5
    c: Coincident(g7,g-1)
    c: Radius(g7) = 1.5
FEATURE [PartDesign::Pad] Pad259  label="M3 Nut Primitive050"
  Length = 1.2
  Length2 = 1.2
  Profile = -> Sketch640
  Type = 4
FEATURE [Sketcher::SketchObject] Sketch642
  MapMode = 5
  Support = -> [XY_Plane186]
  sketch-geometry (8):
    g0: LineSegment StartX=0 StartY=2.3094 StartZ=0 EndX=-2 EndY=1.1547 EndZ=0
    g1: LineSegment StartX=-2 StartY=1.1547 StartZ=0 EndX=-2 EndY=-1.1547 EndZ=0
    g2: LineSegment StartX=-2 StartY=-1.1547 StartZ=0 EndX=-2e-16 EndY=-2.3094 EndZ=0
    g3: LineSegment StartX=-2e-16 StartY=-2.3094 StartZ=0 EndX=2 EndY=-1.1547 EndZ=0
    g4: LineSegment StartX=2 StartY=-1.1547 StartZ=0 EndX=2 EndY=1.1547 EndZ=0
    g5: LineSegment StartX=2 StartY=1.1547 StartZ=0 EndX=0 EndY=2.3094 EndZ=0
    g6: Circle [constr] CenterX=0 CenterY=0 CenterZ=0 NormalX=0 NormalY=0 NormalZ=1 AngleXU=0 Radius=2.3094
    g7: Circle CenterX=0 CenterY=0 CenterZ=0 NormalX=0 NormalY=0 NormalZ=1 AngleXU=0 Radius=1
  constraints (18):
    c: Coincident(g0,g1)
    c: Coincident(g1,g2)
    c: Coincident(g2,g3)
    c: Coincident(g3,g4)
    c: Coincident(g4,g5)
    c: Coincident(g5,g0)
    c: Equal(g0, g1-g5) x5
    c: PointOnObject(g0,g6)
    c: PointOnObject(g1,g6)
    c: PointOnObject(g2,g6)
    c: PointOnObject(g3,g6)
    c: PointOnObject(g4,g6)
    c: PointOnObject(g5,g6)
    c: Coincident(g6,g-1)
    c: PointOnObject(g5,g-2)
    c: DistanceX(g0,g4) = 4
    c: Coincident(g7,g-1)
    c: Radius(g7) = 1
FEATURE [PartDesign::Pad] Pad257  label="M3 Nut Primitive048"
  Length = 0.6
  Length2 = 0.6
  Profile = -> Sketch642
  Type = 4
FEATURE [Sketcher::SketchObject] Sketch643
  MapMode = 5
  Support = -> [XY_Plane186]
FEATURE [Sketcher::SketchObject] Sketch644
  ExternalGeometry = -> [Pad257]
  MapMode = 5
  Placement = pos=(0,0,0) rot=(0.57735,0.57735,0.57735;2.0944rad)
  Support = -> [YZ_Plane186]
  sketch-geometry (6):
    g0: LineSegment StartX=-1.9594 StartY=0.6 StartZ=0 EndX=-2.8094 EndY=0.6 EndZ=0
    g1: LineSegment StartX=-2.8094 StartY=0.6 StartZ=0 EndX=-2.8094 EndY=-0.6 EndZ=0
    g2: LineSegment StartX=-2.8094 StartY=-0.6 StartZ=0 EndX=-1.9594 EndY=-0.6 EndZ=0
    g3: LineSegment StartX=-1.9594 StartY=-0.6 StartZ=0 EndX=-2.3094 EndY=-0.4 EndZ=0
    g4: LineSegment StartX=-2.3094 StartY=-0.4 StartZ=0 EndX=-2.3094 EndY=0.4 EndZ=0
    g5: LineSegment StartX=-2.3094 StartY=0.4 StartZ=0 EndX=-1.9594 EndY=0.6 EndZ=0
  constraints (15):
    c: Horizontal(g0)
    c: Coincident(g0,g1)
    c: Coincident(g1,g2)
    c: Coincident(g2,g3)
    c: Coincident(g3,g4)
    c: Coincident(g4,g5)
    c: Coincident(g5,g0)
    c: Symmetric(g4,g3,g-1)
    c: Symmetric(g0,g2,g-1)
    c: Symmetric(g1,g0,g-1)
    c: DistanceX(g0,g4) = 0.5
    c: DistanceY(g3,g4) = 0.8
    c: DistanceY(g1,g0) = 1.2
    c: PointOnObject(g3,g-3)
    c: DistanceX(g4,g0) = 0.35
FEATURE [PartDesign::Groove] Groove050  label="M3 Nut Smooth048"
  Angle = 360
  Axis = (-2e-16,3e-16,1)
  Base = (0,0,0)
  BaseFeature = -> Pad257
  Profile = -> Sketch644
  ReferenceAxis = -> Sketch644 [V_Axis]
  Reversed = true
FEATURE [PartDesign::Chamfer] Chamfer110  label="M3 Nut Smooth Hole048"
  Base = -> Groove050 [Edge24,Edge23]
  BaseFeature = -> Groove050
  Size = 0.2
FEATURE [Sketcher::SketchObject] Sketch645
  MapMode = 5
  Support = -> [XY_Plane186]
FEATURE [PartDesign::Body] Body129  label="M2 Nut019"
  Group = -> [Sketch642,Pad257,Sketch644,Groove050,Chamfer110,Sketch643,Sketch645]
  Origin = -> Origin211
  Placement = pos=(-19.5,10,15) rot=(0.57735,0.57735,-0.57735;4.18879rad)
  Tip = -> Chamfer110
FEATURE [Sketcher::SketchObject] Sketch646
  MapMode = 5
  Support = -> [XY_Plane184]
  sketch-geometry (1):
    g0: Circle CenterX=0 CenterY=0 CenterZ=0 NormalX=0 NormalY=0 NormalZ=1 AngleXU=0 Radius=1.9
  constraints (2):
    c: Coincident(g0,g-1)
    c: Radius(g0) = 1.9
FEATURE [PartDesign::Pad] Pad227  label="M3x8 Head024"
  Length = 2
  Length2 = 100
  Profile = -> Sketch646
  Type = 0
FEATURE [Sketcher::SketchObject] Sketch631
  MapMode = 5
  Placement = pos=(0,0,2) rot=(0,0,1;0rad)
  Support = -> [Pad227]
  sketch-geometry (1):
    g0: Circle CenterX=0 CenterY=0 CenterZ=0 NormalX=0 NormalY=0 NormalZ=1 AngleXU=0 Radius=1
  constraints (2):
    c: Coincident(g0,g-1)
    c: Radius(g0) = 1
FEATURE [PartDesign::Pad] Pad229  label="M3x8 Thread024"
  BaseFeature = -> Pad227
  Length = 8
  Length2 = 100
  Profile = -> Sketch631
  Type = 0
FEATURE [Sketcher::SketchObject] Sketch628
  MapMode = 5
  Placement = pos=(0,0,0) rot=(1,0,0;3.14159rad)
  Support = -> [Pad229]
  sketch-geometry (7):
    g0: LineSegment StartX=0.77 StartY=0.44456 StartZ=0 EndX=0 EndY=0.889119 EndZ=0
    g1: LineSegment StartX=0 StartY=0.889119 StartZ=0 EndX=-0.77 EndY=0.44456 EndZ=0
    g2: LineSegment StartX=-0.77 StartY=0.44456 StartZ=0 EndX=-0.77 EndY=-0.44456 EndZ=0
    g3: LineSegment StartX=-0.77 StartY=-0.44456 StartZ=0 EndX=3.85628e-11 EndY=-0.889119 EndZ=0
    g4: LineSegment StartX=3.85628e-11 StartY=-0.889119 StartZ=0 EndX=0.77 EndY=-0.44456 EndZ=0
    g5: LineSegment StartX=0.77 StartY=-0.44456 StartZ=0 EndX=0.77 EndY=0.44456 EndZ=0
    g6: Circle [constr] CenterX=0 CenterY=0 CenterZ=0 NormalX=0 NormalY=0 NormalZ=1 AngleXU=0 Radius=0.889119
  constraints (16):
    c: Coincident(g0,g1)
    c: Coincident(g1,g2)
    c: Coincident(g2,g3)
    c: Coincident(g3,g4)
    c: Coincident(g4,g5)
    c: Coincident(g5,g0)
    c: Equal(g0, g1-g5) x5
    c: PointOnObject(g0,g6)
    c: PointOnObject(g1,g6)
    c: PointOnObject(g2,g6)
    c: PointOnObject(g3,g6)
    c: PointOnObject(g4,g6)
    c: PointOnObject(g5,g6)
    c: Coincident(g6,g-1)
    c: PointOnObject(g0,g-2)
    c: DistanceX(g1,g0) = 1.54
FEATURE [PartDesign::Pocket] Pocket254  label="M3x8 Wrench023"
  BaseFeature = -> Pad229
  Length = 1
  Length2 = 100
  Profile = -> Sketch628
  Type = 0
FEATURE [PartDesign::Chamfer] Chamfer096  label="M3x8 Smooth023"
  Base = -> Pocket254 [Face11,Edge2,Edge24,Edge3]
  BaseFeature = -> Pocket254
  Size = 0.2
FEATURE [PartDesign::Body] Body144  label="M2x030"
  Group = -> [Sketch646,Pad227,Sketch631,Pad229,Sketch628,Pocket254,Chamfer096]
  Origin = -> Origin186
  Placement = pos=(-28.75,10,15) rot=(0,1,0;1.5708rad)
  Tip = -> Chamfer096
FEATURE [App::Part] Part059  label="SHOULDER PIN"
  Group = -> [Body129,Body144,Body143]
  Origin = -> Origin204
FEATURE [Sketcher::SketchObject] Sketch648
  MapMode = 5
  Support = -> [XY_Plane185]
  sketch-geometry (8):
    g0: LineSegment StartX=0 StartY=3.17543 StartZ=0 EndX=-2.75 EndY=1.58771 EndZ=0
    g1: LineSegment StartX=-2.75 StartY=1.58771 StartZ=0 EndX=-2.75 EndY=-1.58771 EndZ=0
    g2: LineSegment StartX=-2.75 StartY=-1.58771 StartZ=0 EndX=0 EndY=-3.17543 EndZ=0
    g3: LineSegment StartX=0 StartY=-3.17543 StartZ=0 EndX=2.75 EndY=-1.58771 EndZ=0
    g4: LineSegment StartX=2.75 StartY=-1.58771 StartZ=0 EndX=2.75 EndY=1.58771 EndZ=0
    g5: LineSegment StartX=2.75 StartY=1.58771 StartZ=0 EndX=0 EndY=3.17543 EndZ=0
    g6: Circle [constr] CenterX=0 CenterY=0 CenterZ=0 NormalX=0 NormalY=0 NormalZ=1 AngleXU=0 Radius=3.17543
    g7: Circle CenterX=0 CenterY=0 CenterZ=0 NormalX=0 NormalY=0 NormalZ=1 AngleXU=0 Radius=1.5
  constraints (18):
    c: Coincident(g0,g1)
    c: Coincident(g1,g2)
    c: Coincident(g2,g3)
    c: Coincident(g3,g4)
    c: Coincident(g4,g5)
    c: Coincident(g5,g0)
    c: Equal(g0, g1-g5) x5
    c: PointOnObject(g0,g6)
    c: PointOnObject(g1,g6)
    c: PointOnObject(g2,g6)
    c: PointOnObject(g3,g6)
    c: PointOnObject(g4,g6)
    c: PointOnObject(g5,g6)
    c: Coincident(g6,g-1)
    c: PointOnObject(g5,g-2)
    c: DistanceX(g0,g4) = 5.5
    c: Coincident(g7,g-1)
    c: Radius(g7) = 1.5
FEATURE [PartDesign::Pad] Pad258  label="M3 Nut Primitive049"
  Length = 1.2
  Length2 = 1.2
  Profile = -> Sketch648
  Type = 4
FEATURE [Sketcher::SketchObject] Sketch647
  ExternalGeometry = -> [Pad258]
  MapMode = 5
  Placement = pos=(0,0,0) rot=(0.57735,0.57735,0.57735;2.0944rad)
  Support = -> [YZ_Plane194]
  sketch-geometry (6):
    g0: LineSegment StartX=-2.67543 StartY=1.2 StartZ=0 EndX=-3.67543 EndY=1.2 EndZ=0
    g1: LineSegment StartX=-3.67543 StartY=1.2 StartZ=0 EndX=-3.67543 EndY=-1.2 EndZ=0
    g2: LineSegment StartX=-3.67543 StartY=-1.2 StartZ=0 EndX=-2.67543 EndY=-1.2 EndZ=0
    g3: LineSegment StartX=-2.67543 StartY=-1.2 StartZ=0 EndX=-3.17543 EndY=-1 EndZ=0
    g4: LineSegment StartX=-3.17543 StartY=-1 StartZ=0 EndX=-3.17543 EndY=1 EndZ=0
    g5: LineSegment StartX=-3.17543 StartY=1 StartZ=0 EndX=-2.67543 EndY=1.2 EndZ=0
  constraints (15):
    c: Horizontal(g0)
    c: Coincident(g0,g1)
    c: Coincident(g1,g2)
    c: Coincident(g2,g3)
    c: Coincident(g3,g4)
    c: Coincident(g4,g5)
    c: Coincident(g5,g0)
    c: Symmetric(g4,g3,g-1)
    c: Symmetric(g0,g2,g-1)
    c: Symmetric(g1,g0,g-1)
    c: DistanceX(g0,g4) = 0.5
    c: DistanceY(g3,g4) = 2
    c: DistanceY(g1,g0) = 2.4
    c: PointOnObject(g3,g-3)
    c: DistanceX(g4,g0) = 0.5
FEATURE [PartDesign::Groove] Groove052  label="M3 Nut Smooth050"
  Angle = 360
  Axis = (-2e-16,3e-16,1)
  Base = (0,0,0)
  BaseFeature = -> Pad258
  Profile = -> Sketch647
  ReferenceAxis = -> Sketch647 [V_Axis]
  Reversed = true
FEATURE [PartDesign::Chamfer] Chamfer112  label="M3 Nut Smooth Hole049"
  Base = -> Groove052 [Edge24,Edge23]
  BaseFeature = -> Groove052
  Size = 0.2
FEATURE [PartDesign::Body] Body134  label="M3 Nut023"
  Group = -> [Sketch648,Pad258,Sketch647,Groove052,Chamfer112]
  Origin = -> Origin205
  Placement = pos=(14.15,14.15,3.5) rot=(0,0,-1;0.261799rad)
  Tip = -> Chamfer112
FEATURE [Sketcher::SketchObject] Sketch649
  ExternalGeometry = -> [Pad255]
  MapMode = 5
  Placement = pos=(0,0,0) rot=(0.57735,0.57735,0.57735;2.0944rad)
  Support = -> [YZ_Plane187]
  sketch-geometry (6):
    g0: LineSegment StartX=-2.67543 StartY=1.2 StartZ=0 EndX=-3.67543 EndY=1.2 EndZ=0
    g1: LineSegment StartX=-3.67543 StartY=1.2 StartZ=0 EndX=-3.67543 EndY=-1.2 EndZ=0
    g2: LineSegment StartX=-3.67543 StartY=-1.2 StartZ=0 EndX=-2.67543 EndY=-1.2 EndZ=0
    g3: LineSegment StartX=-2.67543 StartY=-1.2 StartZ=0 EndX=-3.17543 EndY=-1 EndZ=0
    g4: LineSegment StartX=-3.17543 StartY=-1 StartZ=0 EndX=-3.17543 EndY=1 EndZ=0
    g5: LineSegment StartX=-3.17543 StartY=1 StartZ=0 EndX=-2.67543 EndY=1.2 EndZ=0
  constraints (15):
    c: Horizontal(g0)
    c: Coincident(g0,g1)
    c: Coincident(g1,g2)
    c: Coincident(g2,g3)
    c: Coincident(g3,g4)
    c: Coincident(g4,g5)
    c: Coincident(g5,g0)
    c: Symmetric(g4,g3,g-1)
    c: Symmetric(g0,g2,g-1)
    c: Symmetric(g1,g0,g-1)
    c: DistanceX(g0,g4) = 0.5
    c: DistanceY(g3,g4) = 2
    c: DistanceY(g1,g0) = 2.4
    c: PointOnObject(g3,g-3)
    c: DistanceX(g4,g0) = 0.5
FEATURE [PartDesign::Groove] Groove051  label="M3 Nut Smooth049"
  Angle = 360
  Axis = (-2e-16,3e-16,1)
  Base = (0,0,0)
  BaseFeature = -> Pad255
  Profile = -> Sketch649
  ReferenceAxis = -> Sketch649 [V_Axis]
  Reversed = true
FEATURE [PartDesign::Chamfer] Chamfer103  label="M3 Nut Smooth Hole042"
  Base = -> Groove051 [Edge24,Edge23]
  BaseFeature = -> Groove051
  Size = 0.2
FEATURE [PartDesign::Body] Body137  label="M3 Nut025"
  Group = -> [Sketch637,Pad255,Sketch649,Groove051,Chamfer103]
  Origin = -> Origin216
  Placement = pos=(-14.15,14.15,3.5) rot=(0,0,1;0.261799rad)
  Tip = -> Chamfer103
FEATURE [Sketcher::SketchObject] Sketch651
  MapMode = 5
  Support = -> [XY_Plane194]
  sketch-geometry (8):
    g0: LineSegment StartX=0 StartY=3.17543 StartZ=0 EndX=-2.75 EndY=1.58771 EndZ=0
    g1: LineSegment StartX=-2.75 StartY=1.58771 StartZ=0 EndX=-2.75 EndY=-1.58771 EndZ=0
    g2: LineSegment StartX=-2.75 StartY=-1.58771 StartZ=0 EndX=0 EndY=-3.17543 EndZ=0
    g3: LineSegment StartX=0 StartY=-3.17543 StartZ=0 EndX=2.75 EndY=-1.58771 EndZ=0
    g4: LineSegment StartX=2.75 StartY=-1.58771 StartZ=0 EndX=2.75 EndY=1.58771 EndZ=0
    g5: LineSegment StartX=2.75 StartY=1.58771 StartZ=0 EndX=0 EndY=3.17543 EndZ=0
    g6: Circle [constr] CenterX=0 CenterY=0 CenterZ=0 NormalX=0 NormalY=0 NormalZ=1 AngleXU=0 Radius=3.17543
    g7: Circle CenterX=0 CenterY=0 CenterZ=0 NormalX=0 NormalY=0 NormalZ=1 AngleXU=0 Radius=1.5
  constraints (18):
    c: Coincident(g0,g1)
    c: Coincident(g1,g2)
    c: Coincident(g2,g3)
    c: Coincident(g3,g4)
    c: Coincident(g4,g5)
    c: Coincident(g5,g0)
    c: Equal(g0, g1-g5) x5
    c: PointOnObject(g0,g6)
    c: PointOnObject(g1,g6)
    c: PointOnObject(g2,g6)
    c: PointOnObject(g3,g6)
    c: PointOnObject(g4,g6)
    c: PointOnObject(g5,g6)
    c: Coincident(g6,g-1)
    c: PointOnObject(g5,g-2)
    c: DistanceX(g0,g4) = 5.5
    c: Coincident(g7,g-1)
    c: Radius(g7) = 1.5
FEATURE [Sketcher::SketchObject] Sketch652
  ExternalGeometry = -> [Pad259]
  MapMode = 5
  Placement = pos=(0,0,0) rot=(0.57735,0.57735,0.57735;2.0944rad)
  Support = -> [YZ_Plane189]
  sketch-geometry (6):
    g0: LineSegment StartX=-2.67543 StartY=1.2 StartZ=0 EndX=-3.67543 EndY=1.2 EndZ=0
    g1: LineSegment StartX=-3.67543 StartY=1.2 StartZ=0 EndX=-3.67543 EndY=-1.2 EndZ=0
    g2: LineSegment StartX=-3.67543 StartY=-1.2 StartZ=0 EndX=-2.67543 EndY=-1.2 EndZ=0
    g3: LineSegment StartX=-2.67543 StartY=-1.2 StartZ=0 EndX=-3.17543 EndY=-1 EndZ=0
    g4: LineSegment StartX=-3.17543 StartY=-1 StartZ=0 EndX=-3.17543 EndY=1 EndZ=0
    g5: LineSegment StartX=-3.17543 StartY=1 StartZ=0 EndX=-2.67543 EndY=1.2 EndZ=0
  constraints (15):
    c: Horizontal(g0)
    c: Coincident(g0,g1)
    c: Coincident(g1,g2)
    c: Coincident(g2,g3)
    c: Coincident(g3,g4)
    c: Coincident(g4,g5)
    c: Coincident(g5,g0)
    c: Symmetric(g4,g3,g-1)
    c: Symmetric(g0,g2,g-1)
    c: Symmetric(g1,g0,g-1)
    c: DistanceX(g0,g4) = 0.5
    c: DistanceY(g3,g4) = 2
    c: DistanceY(g1,g0) = 2.4
    c: PointOnObject(g3,g-3)
    c: DistanceX(g4,g0) = 0.5
FEATURE [PartDesign::Groove] Groove049  label="M3 Nut Smooth047"
  Angle = 360
  Axis = (-2e-16,3e-16,1)
  Base = (0,0,0)
  BaseFeature = -> Pad259
  Profile = -> Sketch652
  ReferenceAxis = -> Sketch652 [V_Axis]
  Reversed = true
FEATURE [PartDesign::Chamfer] Chamfer105  label="M3 Nut Smooth Hole044"
  Base = -> Groove049 [Edge24,Edge23]
  BaseFeature = -> Groove049
  Size = 0.2
FEATURE [PartDesign::Body] Body130  label="M3 Nut022"
  Group = -> [Sketch640,Pad259,Sketch652,Groove049,Chamfer105]
  Origin = -> Origin214
  Placement = pos=(-14.15,-14.15,3.5) rot=(0,0,-1;0.261799rad)
  Tip = -> Chamfer105
FEATURE [Sketcher::SketchObject] Sketch653
  MapMode = 5
  Support = -> [XY_Plane190]
  sketch-geometry (1):
    g0: Circle CenterX=0 CenterY=0 CenterZ=0 NormalX=0 NormalY=0 NormalZ=1 AngleXU=0 Radius=2.75
  constraints (2):
    c: Coincident(g0,g-1)
    c: Radius(g0) = 2.75
FEATURE [PartDesign::Pad] Pad226  label="M3x8 Head023"
  Length = 3
  Length2 = 100
  Profile = -> Sketch653
  Type = 0
FEATURE [Sketcher::SketchObject] Sketch654
  MapMode = 5
  Placement = pos=(0,0,3) rot=(0,0,1;0rad)
  Support = -> [Pad253]
  sketch-geometry (1):
    g0: Circle CenterX=0 CenterY=0 CenterZ=0 NormalX=0 NormalY=0 NormalZ=1 AngleXU=0 Radius=1.5
  constraints (2):
    c: Coincident(g0,g-1)
    c: Radius(g0) = 1.5
FEATURE [PartDesign::Pad] Pad252  label="M3x8 Thread031"
  BaseFeature = -> Pad253
  Length = 8
  Length2 = 100
  Profile = -> Sketch654
  Type = 0
FEATURE [Sketcher::SketchObject] Sketch641
  MapMode = 5
  Placement = pos=(0,0,0) rot=(1,0,0;3.14159rad)
  Support = -> [Pad252]
  sketch-geometry (7):
    g0: LineSegment StartX=1.275 StartY=0.736122 StartZ=0 EndX=0 EndY=1.47224 EndZ=0
    g1: LineSegment StartX=0 StartY=1.47224 StartZ=0 EndX=-1.275 EndY=0.736122 EndZ=0
    g2: LineSegment StartX=-1.275 StartY=0.736122 StartZ=0 EndX=-1.275 EndY=-0.736122 EndZ=0
    g3: LineSegment StartX=-1.275 StartY=-0.736122 StartZ=0 EndX=1.34766e-11 EndY=-1.47224 EndZ=0
    g4: LineSegment StartX=1.34766e-11 StartY=-1.47224 StartZ=0 EndX=1.275 EndY=-0.736122 EndZ=0
    g5: LineSegment StartX=1.275 StartY=-0.736122 StartZ=0 EndX=1.275 EndY=0.736122 EndZ=0
    g6: Circle [constr] CenterX=0 CenterY=0 CenterZ=0 NormalX=0 NormalY=0 NormalZ=1 AngleXU=0 Radius=1.47224
  constraints (16):
    c: Coincident(g0,g1)
    c: Coincident(g1,g2)
    c: Coincident(g2,g3)
    c: Coincident(g3,g4)
    c: Coincident(g4,g5)
    c: Coincident(g5,g0)
    c: Equal(g0, g1-g5) x5
    c: PointOnObject(g0,g6)
    c: PointOnObject(g1,g6)
    c: PointOnObject(g2,g6)
    c: PointOnObject(g3,g6)
    c: PointOnObject(g4,g6)
    c: PointOnObject(g5,g6)
    c: Coincident(g6,g-1)
    c: PointOnObject(g0,g-2)
    c: DistanceX(g1,g0) = 2.55
FEATURE [PartDesign::Pocket] Pocket265  label="M3x8 Wrench031"
  BaseFeature = -> Pad252
  Length = 1.3
  Length2 = 100
  Profile = -> Sketch641
  Type = 0
FEATURE [PartDesign::Chamfer] Chamfer113  label="M3x8 Smooth031"
  Base = -> Pocket265 [Face11,Edge2,Edge24,Edge3]
  BaseFeature = -> Pocket265
  Size = 0.2
FEATURE [PartDesign::Body] Body135  label="M3x034"
  Group = -> [Sketch638,Pad253,Sketch654,Pad252,Sketch641,Pocket265,Chamfer113]
  Origin = -> Origin215
  Placement = pos=(14.15,14.15,-6) rot=(0,0,1;0rad)
  Tip = -> Chamfer113
FEATURE [Sketcher::SketchObject] Sketch655
  MapMode = 5
  Support = -> [XY_Plane197]
  sketch-geometry (1):
    g0: Circle CenterX=0 CenterY=0 CenterZ=0 NormalX=0 NormalY=0 NormalZ=1 AngleXU=0 Radius=2.75
  constraints (2):
    c: Coincident(g0,g-1)
    c: Radius(g0) = 2.75
FEATURE [PartDesign::Pad] Pad260  label="M3x8 Head033"
  Length = 3
  Length2 = 100
  Profile = -> Sketch655
  Type = 0
FEATURE [Sketcher::SketchObject] Sketch657
  MapMode = 5
  Placement = pos=(0,0,3) rot=(0,0,1;0rad)
  Support = -> [Pad260]
  sketch-geometry (1):
    g0: Circle CenterX=0 CenterY=0 CenterZ=0 NormalX=0 NormalY=0 NormalZ=1 AngleXU=0 Radius=1.5
  constraints (2):
    c: Coincident(g0,g-1)
    c: Radius(g0) = 1.5
FEATURE [PartDesign::Pad] Pad256  label="M3x8 Thread033"
  BaseFeature = -> Pad260
  Length = 8
  Length2 = 100
  Profile = -> Sketch657
  Type = 0
FEATURE [Sketcher::SketchObject] Sketch656
  MapMode = 5
  Placement = pos=(0,0,0) rot=(1,0,0;3.14159rad)
  Support = -> [Pad256]
  sketch-geometry (7):
    g0: LineSegment StartX=1.275 StartY=0.736122 StartZ=0 EndX=0 EndY=1.47224 EndZ=0
    g1: LineSegment StartX=0 StartY=1.47224 StartZ=0 EndX=-1.275 EndY=0.736122 EndZ=0
    g2: LineSegment StartX=-1.275 StartY=0.736122 StartZ=0 EndX=-1.275 EndY=-0.736122 EndZ=0
    g3: LineSegment StartX=-1.275 StartY=-0.736122 StartZ=0 EndX=1.34766e-11 EndY=-1.47224 EndZ=0
    g4: LineSegment StartX=1.34766e-11 StartY=-1.47224 StartZ=0 EndX=1.275 EndY=-0.736122 EndZ=0
    g5: LineSegment StartX=1.275 StartY=-0.736122 StartZ=0 EndX=1.275 EndY=0.736122 EndZ=0
    g6: Circle [constr] CenterX=0 CenterY=0 CenterZ=0 NormalX=0 NormalY=0 NormalZ=1 AngleXU=0 Radius=1.47224
  constraints (16):
    c: Coincident(g0,g1)
    c: Coincident(g1,g2)
    c: Coincident(g2,g3)
    c: Coincident(g3,g4)
    c: Coincident(g4,g5)
    c: Coincident(g5,g0)
    c: Equal(g0, g1-g5) x5
    c: PointOnObject(g0,g6)
    c: PointOnObject(g1,g6)
    c: PointOnObject(g2,g6)
    c: PointOnObject(g3,g6)
    c: PointOnObject(g4,g6)
    c: PointOnObject(g5,g6)
    c: Coincident(g6,g-1)
    c: PointOnObject(g0,g-2)
    c: DistanceX(g1,g0) = 2.55
FEATURE [PartDesign::Pocket] Pocket266  label="M3x8 Wrench032"
  BaseFeature = -> Pad256
  Length = 1.3
  Length2 = 100
  Profile = -> Sketch656
  Type = 0
FEATURE [PartDesign::Chamfer] Chamfer108  label="M3x8 Smooth029"
  Base = -> Pocket266 [Face11,Edge2,Edge24,Edge3]
  BaseFeature = -> Pocket266
  Size = 0.2
FEATURE [PartDesign::Body] Body131  label="M3x031"
  Group = -> [Sketch655,Pad260,Sketch657,Pad256,Sketch656,Pocket266,Chamfer108]
  Origin = -> Origin219
  Placement = pos=(-14.15,-14.15,-6) rot=(0,0,1;0rad)
  Tip = -> Chamfer108
FEATURE [Sketcher::SketchObject] Sketch659
  MapMode = 5
  Support = -> [XY_Plane192]
  sketch-geometry (1):
    g0: Circle CenterX=0 CenterY=0 CenterZ=0 NormalX=0 NormalY=0 NormalZ=1 AngleXU=0 Radius=2.75
  constraints (2):
    c: Coincident(g0,g-1)
    c: Radius(g0) = 2.75
FEATURE [PartDesign::Pad] Pad251  label="M3x8 Head031"
  Length = 3
  Length2 = 100
  Profile = -> Sketch659
  Type = 0
FEATURE [Sketcher::SketchObject] Sketch661
  MapMode = 5
  Placement = pos=(0,0,3) rot=(0,0,1;0rad)
  Support = -> [Pad226]
  sketch-geometry (1):
    g0: Circle CenterX=0 CenterY=0 CenterZ=0 NormalX=0 NormalY=0 NormalZ=1 AngleXU=0 Radius=1.5
  constraints (2):
    c: Coincident(g0,g-1)
    c: Radius(g0) = 1.5
FEATURE [PartDesign::Pad] Pad228  label="M3x8 Thread023"
  BaseFeature = -> Pad226
  Length = 8
  Length2 = 100
  Profile = -> Sketch661
  Type = 0
FEATURE [Sketcher::SketchObject] Sketch658
  MapMode = 5
  Placement = pos=(0,0,0) rot=(1,0,0;3.14159rad)
  Support = -> [Pad228]
  sketch-geometry (7):
    g0: LineSegment StartX=1.275 StartY=0.736122 StartZ=0 EndX=0 EndY=1.47224 EndZ=0
    g1: LineSegment StartX=0 StartY=1.47224 StartZ=0 EndX=-1.275 EndY=0.736122 EndZ=0
    g2: LineSegment StartX=-1.275 StartY=0.736122 StartZ=0 EndX=-1.275 EndY=-0.736122 EndZ=0
    g3: LineSegment StartX=-1.275 StartY=-0.736122 StartZ=0 EndX=1.34766e-11 EndY=-1.47224 EndZ=0
    g4: LineSegment StartX=1.34766e-11 StartY=-1.47224 StartZ=0 EndX=1.275 EndY=-0.736122 EndZ=0
    g5: LineSegment StartX=1.275 StartY=-0.736122 StartZ=0 EndX=1.275 EndY=0.736122 EndZ=0
    g6: Circle [constr] CenterX=0 CenterY=0 CenterZ=0 NormalX=0 NormalY=0 NormalZ=1 AngleXU=0 Radius=1.47224
  constraints (16):
    c: Coincident(g0,g1)
    c: Coincident(g1,g2)
    c: Coincident(g2,g3)
    c: Coincident(g3,g4)
    c: Coincident(g4,g5)
    c: Coincident(g5,g0)
    c: Equal(g0, g1-g5) x5
    c: PointOnObject(g0,g6)
    c: PointOnObject(g1,g6)
    c: PointOnObject(g2,g6)
    c: PointOnObject(g3,g6)
    c: PointOnObject(g4,g6)
    c: PointOnObject(g5,g6)
    c: Coincident(g6,g-1)
    c: PointOnObject(g0,g-2)
    c: DistanceX(g1,g0) = 2.55
FEATURE [PartDesign::Pocket] Pocket255  label="M3x8 Wrench024"
  BaseFeature = -> Pad228
  Length = 1.3
  Length2 = 100
  Profile = -> Sketch658
  Type = 0
FEATURE [Sketcher::SketchObject] Sketch662
  MapMode = 5
  Placement = pos=(0,0,3) rot=(0,0,1;0rad)
  Support = -> [Pad251]
  sketch-geometry (1):
    g0: Circle CenterX=0 CenterY=0 CenterZ=0 NormalX=0 NormalY=0 NormalZ=1 AngleXU=0 Radius=1.5
  constraints (2):
    c: Coincident(g0,g-1)
    c: Radius(g0) = 1.5
FEATURE [PartDesign::Pad] Pad254  label="M3x8 Thread032"
  BaseFeature = -> Pad251
  Length = 8
  Length2 = 100
  Profile = -> Sketch662
  Type = 0
FEATURE [Sketcher::SketchObject] Sketch660
  MapMode = 5
  Placement = pos=(0,0,0) rot=(1,0,0;3.14159rad)
  Support = -> [Pad254]
  sketch-geometry (7):
    g0: LineSegment StartX=1.275 StartY=0.736122 StartZ=0 EndX=0 EndY=1.47224 EndZ=0
    g1: LineSegment StartX=0 StartY=1.47224 StartZ=0 EndX=-1.275 EndY=0.736122 EndZ=0
    g2: LineSegment StartX=-1.275 StartY=0.736122 StartZ=0 EndX=-1.275 EndY=-0.736122 EndZ=0
    g3: LineSegment StartX=-1.275 StartY=-0.736122 StartZ=0 EndX=1.34766e-11 EndY=-1.47224 EndZ=0
    g4: LineSegment StartX=1.34766e-11 StartY=-1.47224 StartZ=0 EndX=1.275 EndY=-0.736122 EndZ=0
    g5: LineSegment StartX=1.275 StartY=-0.736122 StartZ=0 EndX=1.275 EndY=0.736122 EndZ=0
    g6: Circle [constr] CenterX=0 CenterY=0 CenterZ=0 NormalX=0 NormalY=0 NormalZ=1 AngleXU=0 Radius=1.47224
  constraints (16):
    c: Coincident(g0,g1)
    c: Coincident(g1,g2)
    c: Coincident(g2,g3)
    c: Coincident(g3,g4)
    c: Coincident(g4,g5)
    c: Coincident(g5,g0)
    c: Equal(g0, g1-g5) x5
    c: PointOnObject(g0,g6)
    c: PointOnObject(g1,g6)
    c: PointOnObject(g2,g6)
    c: PointOnObject(g3,g6)
    c: PointOnObject(g4,g6)
    c: PointOnObject(g5,g6)
    c: Coincident(g6,g-1)
    c: PointOnObject(g0,g-2)
    c: DistanceX(g1,g0) = 2.55
FEATURE [PartDesign::Pocket] Pocket267  label="M3x8 Wrench033"
  BaseFeature = -> Pad254
  Length = 1.3
  Length2 = 100
  Profile = -> Sketch660
  Type = 0
FEATURE [PartDesign::Chamfer] Chamfer097  label="M3x8 Smooth024"
  Base = -> Pocket267 [Face11,Edge2,Edge24,Edge3]
  BaseFeature = -> Pocket267
  Size = 0.2
FEATURE [PartDesign::Body] Body132  label="M3x032"
  Group = -> [Sketch659,Pad251,Sketch662,Pad254,Sketch660,Pocket267,Chamfer097]
  Origin = -> Origin207
  Placement = pos=(-14.15,14.15,-6) rot=(0,0,1;0rad)
  Tip = -> Chamfer097
FEATURE [Sketcher::SketchObject] Sketch663
  ExternalGeometry = -> [Pad238]
  MapMode = 5
  Placement = pos=(0,0,0) rot=(0.57735,0.57735,0.57735;2.0944rad)
  Support = -> [YZ_Plane217]
  sketch-geometry (6):
    g0: LineSegment StartX=-1.9594 StartY=0.6 StartZ=0 EndX=-2.8094 EndY=0.6 EndZ=0
    g1: LineSegment StartX=-2.8094 StartY=0.6 StartZ=0 EndX=-2.8094 EndY=-0.6 EndZ=0
    g2: LineSegment StartX=-2.8094 StartY=-0.6 StartZ=0 EndX=-1.9594 EndY=-0.6 EndZ=0
    g3: LineSegment StartX=-1.9594 StartY=-0.6 StartZ=0 EndX=-2.3094 EndY=-0.4 EndZ=0
    g4: LineSegment StartX=-2.3094 StartY=-0.4 StartZ=0 EndX=-2.3094 EndY=0.4 EndZ=0
    g5: LineSegment StartX=-2.3094 StartY=0.4 StartZ=0 EndX=-1.9594 EndY=0.6 EndZ=0
  constraints (15):
    c: Horizontal(g0)
    c: Coincident(g0,g1)
    c: Coincident(g1,g2)
    c: Coincident(g2,g3)
    c: Coincident(g3,g4)
    c: Coincident(g4,g5)
    c: Coincident(g5,g0)
    c: Symmetric(g4,g3,g-1)
    c: Symmetric(g0,g2,g-1)
    c: Symmetric(g1,g0,g-1)
    c: DistanceX(g0,g4) = 0.5
    c: DistanceY(g3,g4) = 0.8
    c: DistanceY(g1,g0) = 1.2
    c: PointOnObject(g3,g-3)
    c: DistanceX(g4,g0) = 0.35
FEATURE [PartDesign::Groove] Groove044  label="M3 Nut Smooth042"
  Angle = 360
  Axis = (-2e-16,3e-16,1)
  Base = (0,0,0)
  BaseFeature = -> Pad238
  Profile = -> Sketch663
  ReferenceAxis = -> Sketch663 [V_Axis]
  Reversed = true
FEATURE [PartDesign::Chamfer] Chamfer115  label="M3 Nut Smooth Hole050"
  Base = -> Groove044 [Edge24,Edge23]
  BaseFeature = -> Groove044
  Size = 0.2
FEATURE [PartDesign::Body] Body140  label="M2 Nut020"
  Group = -> [Sketch602,Pad238,Sketch663,Groove044,Chamfer115,Sketch572,Sketch573]
  Origin = -> Origin202
  Placement = pos=(0,0,2.75) rot=(0,0,1;0rad)
  Tip = -> Chamfer115
FEATURE [App::Part] Part058  label="M022"
  Group = -> [Body139,Body140]
  Origin = -> Origin184
  Placement = pos=(-9.8e-15,10.5,80) rot=(0,1,0;3.14159rad)
FEATURE [App::Part] Part056  label="Screws004"
  Group = -> [Part058,Part057,Part055,Part060,Part061,Part062]
  Origin = -> Origin206
  Placement = pos=(0,0,-71) rot=(0,0,1;0rad)
FEATURE [PartDesign::Pad] Pad261  label="Baseplate011"
  Length = 5
  Length2 = 100
  Profile = -> Sketch588
  Type = 0
FEATURE [PartDesign::Pad] Pad262  label="Baseplate Expansion"
  BaseFeature = -> Pad261
  Length = 20
  Length2 = 100
  Profile = -> Pad261 [Face10]
  Type = 0
FEATURE [Sketcher::SketchObject] Sketch583
  MapMode = 5
  Placement = pos=(0,0,25) rot=(0,0,1;0rad)
  Support = -> [Pad262]
  sketch-geometry (8):
    g0: LineSegment StartX=9.75 StartY=28.25 StartZ=0 EndX=9.75 EndY=20.25 EndZ=0
    g1: LineSegment StartX=9.75 StartY=20.25 StartZ=0 EndX=-18.75 EndY=20.25 EndZ=0
    g2: LineSegment StartX=-18.75 StartY=20.25 StartZ=0 EndX=-18.75 EndY=-20.25 EndZ=0
    g3: LineSegment StartX=-18.75 StartY=-20.25 StartZ=0 EndX=9.75 EndY=-20.25 EndZ=0
    g4: LineSegment StartX=9.75 StartY=-20.25 StartZ=0 EndX=9.75 EndY=-28.25 EndZ=0
    g5: LineSegment StartX=9.75 StartY=-28.25 StartZ=0 EndX=21.75 EndY=-28.25 EndZ=0
    g6: LineSegment StartX=21.75 StartY=-28.25 StartZ=0 EndX=21.75 EndY=28.25 EndZ=0
    g7: LineSegment StartX=21.75 StartY=28.25 StartZ=0 EndX=9.75 EndY=28.25 EndZ=0
  constraints (22):
    c: Vertical(g0)
    c: Coincident(g0,g1)
    c: Horizontal(g1)
    c: Coincident(g1,g2)
    c: Coincident(g2,g3)
    c: Horizontal(g3)
    c: Coincident(g3,g4)
    c: Vertical(g4)
    c: Coincident(g4,g5)
    c: Horizontal(g5)
    c: Coincident(g5,g6)
    c: Coincident(g6,g7)
    c: Coincident(g7,g0)
    c: Horizontal(g7)
    c: Equal(g7,g5)
    c: Symmetric(g6,g5,g-1)
    c: Symmetric(g1,g2,g-1)
    c: DistanceY(g6,g6) = 56.5
    c: DistanceX(g-1,g6) = 21.75
    c: DistanceX(g1,g-1) = 18.75
    c: DistanceY(g0,g0) = 8
    c: DistanceX(g1,g0) = 28.5
FEATURE [PartDesign::Pocket] Pocket272  label="Servo Pocket004"
  BaseFeature = -> Pad262
  Length = 20
  Length2 = 100
  Profile = -> Sketch583
  Type = 0
FEATURE [Sketcher::SketchObject] Sketch587
  MapMode = 5
  Placement = pos=(0,0,5) rot=(0,0,1;0rad)
  Support = -> [Pocket272]
  sketch-geometry (1):
    g0: Circle CenterX=0 CenterY=0 CenterZ=0 NormalX=0 NormalY=0 NormalZ=1 AngleXU=0 Radius=16.5
  constraints (2):
    c: Coincident(g0,g-1)
    c: Radius(g0) = 16.5
FEATURE [PartDesign::Pocket] Pocket268  label="Accesshole Servohorn Cap"
  BaseFeature = -> Pocket272
  Length = 5
  Length2 = 100
  Profile = -> Sketch587
  Type = 0
FEATURE [Sketcher::SketchObject] Sketch581
  MapMode = 5
  Placement = pos=(0,0,5) rot=(0,0,1;0rad)
  Support = -> [Pocket268]
  sketch-geometry (9):
    g0: Circle [constr] CenterX=0 CenterY=0 CenterZ=0 NormalX=0 NormalY=0 NormalZ=1 AngleXU=0 Radius=20
    g1: LineSegment [constr] StartX=-14.1421 StartY=14.1421 StartZ=0 EndX=14.1421 EndY=14.1421 EndZ=0
    g2: LineSegment [constr] StartX=14.1421 StartY=14.1421 StartZ=0 EndX=14.1421 EndY=-14.1421 EndZ=0
    g3: LineSegment [constr] StartX=14.1421 StartY=-14.1421 StartZ=0 EndX=-14.1421 EndY=-14.1421 EndZ=0
    g4: LineSegment [constr] StartX=-14.1421 StartY=-14.1421 StartZ=0 EndX=-14.1421 EndY=14.1421 EndZ=0
    g5: Circle CenterX=-14.1421 CenterY=14.1421 CenterZ=0 NormalX=0 NormalY=0 NormalZ=1 AngleXU=0 Radius=1.6
    g6: Circle CenterX=14.1421 CenterY=14.1421 CenterZ=0 NormalX=0 NormalY=0 NormalZ=1 AngleXU=0 Radius=1.6
    g7: Circle CenterX=14.1421 CenterY=-14.1421 CenterZ=0 NormalX=0 NormalY=0 NormalZ=1 AngleXU=0 Radius=1.6
    g8: Circle CenterX=-14.1421 CenterY=-14.1421 CenterZ=0 NormalX=0 NormalY=0 NormalZ=1 AngleXU=0 Radius=1.6
  constraints (22):
    c: Coincident(g0,g-1)
    c: Radius(g0) = 20
    c: Coincident(g1,g2)
    c: Coincident(g2,g3)
    c: Coincident(g3,g4)
    c: Coincident(g4,g1)
    c: Horizontal(g1)
    c: Horizontal(g3)
    c: Vertical(g2)
    c: Vertical(g4)
    c: PointOnObject(g1,g0)
    c: PointOnObject(g2,g0)
    c: PointOnObject(g1,g0)
    c: Equal(g1,g2)
    c: Coincident(g5,g1)
    c: Coincident(g6,g1)
    c: Coincident(g7,g2)
    c: Coincident(g8,g3)
    c: Radius(g5) = 1.6
    c: Equal(g5,g6)
    c: Equal(g5,g7)
    c: Equal(g5,g8)
FEATURE [PartDesign::Pocket] Pocket253  label="Screwholes Servohorn Cap"
  BaseFeature = -> Pocket268
  Length = 5
  Length2 = 100
  Profile = -> Sketch581
  Type = 0
FEATURE [Sketcher::SketchObject] Sketch585
  MapMode = 5
  Placement = pos=(0,0,5) rot=(0,0,1;0rad)
  Support = -> [Pocket253]
  sketch-geometry (35):
    g0: Circle [constr] CenterX=0 CenterY=0 CenterZ=0 NormalX=0 NormalY=0 NormalZ=1 AngleXU=0 Radius=20
    g1: LineSegment [constr] StartX=-14.1421 StartY=14.1421 StartZ=0 EndX=14.1421 EndY=-14.1421 EndZ=0
    g2: LineSegment [constr] StartX=14.1421 StartY=14.1421 StartZ=0 EndX=-14.1421 EndY=-14.1421 EndZ=0
    g3: LineSegment [constr] StartX=-14.1421 StartY=14.1421 StartZ=0 EndX=14.1421 EndY=14.1421 EndZ=0
    g4: LineSegment [constr] StartX=14.1421 StartY=14.1421 StartZ=0 EndX=14.1421 EndY=-14.1421 EndZ=0
    g5: LineSegment [constr] StartX=14.1421 StartY=-14.1421 StartZ=0 EndX=-14.1421 EndY=-14.1421 EndZ=0
    g6: LineSegment [constr] StartX=-14.1421 StartY=-14.1421 StartZ=0 EndX=-14.1421 EndY=14.1421 EndZ=0
    g7: LineSegment StartX=-11.8151 StartY=16.4692 StartZ=0 EndX=-14.9939 EndY=17.3209 EndZ=0
    g8: LineSegment StartX=-14.9939 StartY=17.3209 StartZ=0 EndX=-17.3209 EndY=14.9939 EndZ=0
    g9: LineSegment StartX=-17.3209 StartY=14.9939 StartZ=0 EndX=-16.4692 EndY=11.8151 EndZ=0
    g10: LineSegment StartX=-16.4692 StartY=11.8151 StartZ=0 EndX=-13.2904 EndY=10.9634 EndZ=0
    g11: LineSegment StartX=-13.2904 StartY=10.9634 StartZ=0 EndX=-10.9634 EndY=13.2904 EndZ=0
    g12: LineSegment StartX=-10.9634 StartY=13.2904 StartZ=0 EndX=-11.8151 EndY=16.4692 EndZ=0
    g13: Circle [constr] CenterX=-14.1421 CenterY=14.1421 CenterZ=0 NormalX=0 NormalY=0 NormalZ=1 AngleXU=0 Radius=3.2909
    g14: LineSegment StartX=14.9939 StartY=17.3209 StartZ=0 EndX=11.8151 EndY=16.4692 EndZ=0
    g15: LineSegment StartX=11.8151 StartY=16.4692 StartZ=0 EndX=10.9634 EndY=13.2904 EndZ=0
    g16: LineSegment StartX=10.9634 StartY=13.2904 StartZ=0 EndX=13.2904 EndY=10.9634 EndZ=0
    g17: LineSegment StartX=13.2904 StartY=10.9634 StartZ=0 EndX=16.4692 EndY=11.8151 EndZ=0
    g18: LineSegment StartX=16.4692 StartY=11.8151 StartZ=0 EndX=17.3209 EndY=14.9939 EndZ=0
    g19: LineSegment StartX=17.3209 StartY=14.9939 StartZ=0 EndX=14.9939 EndY=17.3209 EndZ=0
    g20: Circle [constr] CenterX=14.1421 CenterY=14.1421 CenterZ=0 NormalX=0 NormalY=0 NormalZ=1 AngleXU=0 Radius=3.2909
    g21: LineSegment StartX=-13.2904 StartY=-10.9634 StartZ=0 EndX=-16.4692 EndY=-11.8151 EndZ=0
    g22: LineSegment StartX=-16.4692 StartY=-11.8151 StartZ=0 EndX=-17.3209 EndY=-14.9939 EndZ=0
    g23: LineSegment StartX=-17.3209 StartY=-14.9939 StartZ=0 EndX=-14.9939 EndY=-17.3209 EndZ=0
    g24: LineSegment StartX=-14.9939 StartY=-17.3209 StartZ=0 EndX=-11.8151 EndY=-16.4692 EndZ=0
    g25: LineSegment StartX=-11.8151 StartY=-16.4692 StartZ=0 EndX=-10.9634 EndY=-13.2904 EndZ=0
    g26: LineSegment StartX=-10.9634 StartY=-13.2904 StartZ=0 EndX=-13.2904 EndY=-10.9634 EndZ=0
    g27: Circle [constr] CenterX=-14.1421 CenterY=-14.1421 CenterZ=0 NormalX=0 NormalY=0 NormalZ=1 AngleXU=0 Radius=3.2909
    g28: LineSegment StartX=16.4692 StartY=-11.8151 StartZ=0 EndX=13.2904 EndY=-10.9634 EndZ=0
    g29: LineSegment StartX=13.2904 StartY=-10.9634 StartZ=0 EndX=10.9634 EndY=-13.2904 EndZ=0
    g30: LineSegment StartX=10.9634 StartY=-13.2904 StartZ=0 EndX=11.8151 EndY=-16.4692 EndZ=0
    g31: LineSegment StartX=11.8151 StartY=-16.4692 StartZ=0 EndX=14.9939 EndY=-17.3209 EndZ=0
    g32: LineSegment StartX=14.9939 StartY=-17.3209 StartZ=0 EndX=17.3209 EndY=-14.9939 EndZ=0
    g33: LineSegment StartX=17.3209 StartY=-14.9939 StartZ=0 EndX=16.4692 EndY=-11.8151 EndZ=0
    g34: Circle [constr] CenterX=14.1421 CenterY=-14.1421 CenterZ=0 NormalX=0 NormalY=0 NormalZ=1 AngleXU=0 Radius=3.2909
  constraints (84):
    c: Coincident(g0,g-1)
    c: Radius(g0) = 20
    c: PointOnObject(g1,g0)
    c: PointOnObject(g1,g0)
    c: PointOnObject(g2,g0)
    c: PointOnObject(g2,g0)
    c: PointOnObject(g-1,g2)
    c: PointOnObject(g-1,g1)
    c: Perpendicular(g1,g2)
    c: Coincident(g3,g4)
    c: Coincident(g4,g5)
    c: Coincident(g5,g6)
    c: Coincident(g6,g3)
    c: Horizontal(g3)
    c: Horizontal(g5)
    c: Vertical(g4)
    c: Vertical(g6)
    c: Coincident(g3,g1)
    c: Coincident(g4,g1)
    c: Equal(g3,g4)
    c: Coincident(g7,g8)
    c: Coincident(g8,g9)
    c: Coincident(g9,g10)
    c: Coincident(g10,g11)
    c: Coincident(g11,g12)
    c: Coincident(g12,g7)
    c: Equal(g7, g8-g12) x5
    c: PointOnObject(g7,g13)
    c: PointOnObject(g8,g13)
    c: PointOnObject(g9,g13)
    c: PointOnObject(g10,g13)
    c: PointOnObject(g11,g13)
    c: PointOnObject(g12,g13)
    c: Coincident(g13,g1)
    c: Coincident(g14,g15)
    c: Coincident(g15,g16)
    c: Coincident(g16,g17)
    c: Coincident(g17,g18)
    c: Coincident(g18,g19)
    c: Coincident(g19,g14)
    c: Equal(g14, g15-g19) x5
    c: PointOnObject(g14,g20)
    c: PointOnObject(g15,g20)
    c: PointOnObject(g16,g20)
    c: PointOnObject(g17,g20)
    c: PointOnObject(g18,g20)
    c: PointOnObject(g19,g20)
    c: Coincident(g20,g2)
    c: Coincident(g21,g22)
    c: Coincident(g22,g23)
    c: Coincident(g23,g24)
    c: Coincident(g24,g25)
    c: Coincident(g25,g26)
    c: Coincident(g26,g21)
    c: Equal(g21, g22-g26) x5
    c: PointOnObject(g21,g27)
    c: PointOnObject(g22,g27)
    c: PointOnObject(g23,g27)
    c: PointOnObject(g24,g27)
    c: PointOnObject(g25,g27)
    c: PointOnObject(g26,g27)
    c: Coincident(g27,g2)
    c: Perpendicular(g1,g11)
    c: Perpendicular(g2,g16)
    c: Perpendicular(g2,g26)
    c: Coincident(g28,g29)
    c: Coincident(g29,g30)
    c: Coincident(g30,g31)
    c: Coincident(g31,g32)
    c: Coincident(g32,g33)
    c: Coincident(g33,g28)
    c: Equal(g28, g29-g33) x5
    c: PointOnObject(g28,g34)
    c: PointOnObject(g29,g34)
    c: PointOnObject(g30,g34)
    c: PointOnObject(g31,g34)
    c: PointOnObject(g32,g34)
    c: PointOnObject(g33,g34)
    c: Coincident(g34,g1)
    c: Perpendicular(g1,g29)
    c: Equal(g20,g13)
    c: Equal(g13,g27)
    c: Equal(g27,g34)
    c: Distance(g15,g14) = 5.7
FEATURE [PartDesign::Pocket] Pocket269  label="Nutholes Servohorn Cap"
  BaseFeature = -> Pocket253
  Length = 2.5
  Length2 = 100
  Profile = -> Sketch585
  Type = 0
FEATURE [Sketcher::SketchObject] Sketch577
  MapMode = 5
  Placement = pos=(0,-28.25,0) rot=(1,0,0;1.5708rad)
  Support = -> [Pocket269]
  sketch-geometry (8):
    g0: LineSegment StartX=3.75 StartY=22.9 StartZ=0 EndX=6.75 EndY=22.9 EndZ=0
    g1: LineSegment StartX=6.75 StartY=22.9 StartZ=0 EndX=6.75 EndY=17.1 EndZ=0
    g2: LineSegment StartX=6.75 StartY=17.1 StartZ=0 EndX=3.75 EndY=17.1 EndZ=0
    g3: LineSegment StartX=3.75 StartY=17.1 StartZ=0 EndX=3.75 EndY=22.9 EndZ=0
    g4: LineSegment StartX=3.75 StartY=12.9 StartZ=0 EndX=6.75 EndY=12.9 EndZ=0
    g5: LineSegment StartX=6.75 StartY=12.9 StartZ=0 EndX=6.75 EndY=7.1 EndZ=0
    g6: LineSegment StartX=6.75 StartY=7.1 StartZ=0 EndX=3.75 EndY=7.1 EndZ=0
    g7: LineSegment StartX=3.75 StartY=7.1 StartZ=0 EndX=3.75 EndY=12.9 EndZ=0
  constraints (24):
    c: Coincident(g0,g1)
    c: Coincident(g1,g2)
    c: Coincident(g2,g3)
    c: Coincident(g3,g0)
    c: Horizontal(g0)
    c: Horizontal(g2)
    c: Vertical(g1)
    c: Vertical(g3)
    c: Coincident(g4,g5)
    c: Coincident(g5,g6)
    c: Coincident(g6,g7)
    c: Coincident(g7,g4)
    c: Horizontal(g4)
    c: Horizontal(g6)
    c: Vertical(g5)
    c: Vertical(g7)
    c: Equal(g0,g4)
    c: Equal(g1,g5)
    c: DistanceY(g1,g1) = 5.8
    c: DistanceY(g4,g1) = 4.2
    c: DistanceX(g-1,g5) = 6.75
    c: DistanceX(g0,g0) = 3
    c: Vertical(g4,g1)
    c: DistanceY(g-1,g5) = 7.1
FEATURE [PartDesign::Pocket] Pocket271  label="Nutholes Servo Pocket"
  BaseFeature = -> Pocket269
  Length = 56.5
  Length2 = 100
  Profile = -> Sketch577
  Type = 0
FEATURE [Sketcher::SketchObject] Sketch582
  MapMode = 5
  Placement = pos=(9.75,0,0) rot=(0.57735,0.57735,0.57735;2.0944rad)
  Support = -> [Pocket271]
  sketch-geometry (4):
    g0: Circle CenterX=-24.25 CenterY=20 CenterZ=0 NormalX=0 NormalY=0 NormalZ=1 AngleXU=0 Radius=1.6
    g1: Circle CenterX=-24.25 CenterY=10 CenterZ=0 NormalX=0 NormalY=0 NormalZ=1 AngleXU=0 Radius=1.6
    g2: Circle CenterX=24.25 CenterY=20 CenterZ=0 NormalX=0 NormalY=0 NormalZ=1 AngleXU=0 Radius=1.6
    g3: Circle CenterX=24.25 CenterY=10 CenterZ=0 NormalX=0 NormalY=0 NormalZ=1 AngleXU=0 Radius=1.6
  constraints (11):
    c: Vertical(g3,g2)
    c: Vertical(g1,g0)
    c: Symmetric(g0,g2,g-2)
    c: Radius(g0) = 1.6
    c: Equal(g0,g1)
    c: Equal(g0,g2)
    c: Equal(g0,g3)
    c: DistanceY(g3,g2) = 10
    c: Horizontal(g1,g3)
    c: DistanceY(g-1,g3) = 10
    c: DistanceX(g0,g2) = 48.5
FEATURE [PartDesign::Pocket] Pocket270  label="Screwholes Servo Pocket"
  BaseFeature = -> Pocket271
  Length = 18
  Length2 = 100
  Profile = -> Sketch582
  Type = 0
FEATURE [Sketcher::SketchObject] Sketch584
  MapMode = 5
  Placement = pos=(-18.75,0,0) rot=(0.57735,0.57735,0.57735;2.0944rad)
  Support = -> [Pocket270]
  sketch-geometry (1):
    g0: Circle CenterX=10 CenterY=15 CenterZ=0 NormalX=0 NormalY=0 NormalZ=1 AngleXU=0 Radius=0.95
  constraints (3):
    c: DistanceY(g-1,g0) = 15
    c: DistanceX(g-1,g0) = 10
    c: Radius(g0) = 0.95
FEATURE [PartDesign::Pocket] Pocket006  label="Screwhole Ball Bearing Pin"
  BaseFeature = -> Pocket270
  Length = 3
  Length2 = 100
  Profile = -> Sketch584
  Type = 0
FEATURE [Sketcher::SketchObject] Sketch586
  MapMode = 5
  Placement = pos=(-18.75,0,0) rot=(0.57735,0.57735,0.57735;2.0944rad)
  Support = -> [Pocket006]
  sketch-geometry (7):
    g0: LineSegment StartX=12.05 StartY=13.8164 StartZ=0 EndX=12.05 EndY=16.1836 EndZ=0
    g1: LineSegment StartX=12.05 StartY=16.1836 StartZ=0 EndX=10 EndY=17.3671 EndZ=0
    g2: LineSegment StartX=10 StartY=17.3671 StartZ=0 EndX=7.95 EndY=16.1836 EndZ=0
    g3: LineSegment StartX=7.95 StartY=16.1836 StartZ=0 EndX=7.95 EndY=13.8164 EndZ=0
    g4: LineSegment StartX=7.95 StartY=13.8164 StartZ=0 EndX=10 EndY=12.6329 EndZ=0
    g5: LineSegment StartX=10 StartY=12.6329 StartZ=0 EndX=12.05 EndY=13.8164 EndZ=0
    g6: Circle [constr] CenterX=10 CenterY=15 CenterZ=0 NormalX=0 NormalY=0 NormalZ=1 AngleXU=0 Radius=2.36714
  constraints (17):
    c: Coincident(g0,g1)
    c: Coincident(g1,g2)
    c: Coincident(g2,g3)
    c: Coincident(g3,g4)
    c: Coincident(g4,g5)
    c: Coincident(g5,g0)
    c: Equal(g0, g1-g5) x5
    c: PointOnObject(g0,g6)
    c: PointOnObject(g1,g6)
    c: PointOnObject(g2,g6)
    c: PointOnObject(g3,g6)
    c: PointOnObject(g4,g6)
    c: PointOnObject(g5,g6)
    c: Vertical(g3)
    c: DistanceX(g-1,g6) = 10
    c: DistanceY(g-1,g6) = 15
    c: Distance(g0,g4) = 4.1
FEATURE [PartDesign::Pocket] Pocket007  label="Nuthole Ball Bearing Pin"
  BaseFeature = -> Pocket006
  Length = 1.5
  Length2 = 100
  Profile = -> Sketch586
  Type = 0
FEATURE [Sketcher::SketchObject] Sketch578
  MapMode = 5
  Placement = pos=(0,28.25,0) rot=(0,0.707107,0.707107;3.14159rad)
  Support = -> [Pocket007]
  sketch-geometry (4):
    g0: LineSegment StartX=9.25 StartY=25 StartZ=0 EndX=14.25 EndY=25 EndZ=0
    g1: LineSegment StartX=14.25 StartY=25 StartZ=0 EndX=14.25 EndY=11.5 EndZ=0
    g2: ArcOfCircle CenterX=11.75 CenterY=11.5 CenterZ=0 NormalX=0 NormalY=0 NormalZ=1 AngleXU=0 Radius=2.5 StartAngle=3.14159 EndAngle=6.28319
    g3: LineSegment StartX=9.25 StartY=11.5 StartZ=0 EndX=9.25 EndY=25 EndZ=0
  constraints (11):
    c: Horizontal(g0)
    c: Coincident(g0,g1)
    c: Vertical(g1)
    c: Tangent(g1,g2) = 1.5708
    c: Tangent(g2,g3) = 1.5708
    c: Coincident(g3,g0)
    c: DistanceX(g0,g0) = 5
    c: Vertical(g3)
    c: DistanceX(g-1,g2) = 11.75
    c: DistanceY(g-1,g2) = 11.5
    c: DistanceY(g1,g1) = 13.5
FEATURE [PartDesign::Pocket] Pocket008  label="Servocable004"
  BaseFeature = -> Pocket007
  Length = 8
  Length2 = 100
  Profile = -> Sketch578
  Type = 0
FEATURE [PartDesign::Fillet] Fillet082  label="Smooth Servo Pocket Edges"
  Base = -> Pocket008 [Edge62,Edge137,Edge61,Edge146,Edge60]
  BaseFeature = -> Pocket008
  Radius = 1
FEATURE [PartDesign::Fillet] Fillet081  label="Smooth Servocable Edges002"
  Base = -> Fillet082 [Edge10,Edge165]
  BaseFeature = -> Fillet082
  Radius = 2.5
FEATURE [PartDesign::Body] Body001  label="Shoulder_Joint_Servomount"
  Group = -> [Sketch588,Pad261,Pad262,Sketch583,Pocket272,Sketch587,Pocket268,Sketch581,Pocket253,Sketch585,Pocket269,Sketch577,Pocket271,Sketch582,Pocket270,Sketch584,Pocket006,Sketch586,Pocket007,Sketch578,Pocket008,Fillet082,Fillet081]
  Origin = -> Origin001
  Tip = -> Fillet081
FEATURE [PartDesign::Chamfer] Chamfer117  label="M3x8 Smooth033"
  Base = -> Pocket255 [Face11,Edge2,Edge24,Edge3]
  BaseFeature = -> Pocket255
  Size = 0.2
FEATURE [PartDesign::Body] Body133  label="M3x033"
  Group = -> [Sketch653,Pad226,Sketch661,Pad228,Sketch658,Pocket255,Chamfer117]
  Origin = -> Origin187
  Placement = pos=(14.15,-14.15,-6) rot=(0,0,1;0rad)
  Tip = -> Chamfer117
FEATURE [App::Part] Part051  label="Shouldercap Screws"
  Group = -> [Body135,Body133,Body132,Body131]
  Origin = -> Origin196
FEATURE [PartDesign::Pad] Pad263  label="Baseplate012"
  Length = 12
  Length2 = 100
  Profile = -> Sketch593
  Type = 0
FEATURE [Sketcher::SketchObject] Sketch590
  MapMode = 5
  Placement = pos=(0,0,12) rot=(0,0,1;0rad)
  Support = -> [Pad263]
  sketch-geometry (9):
    g0: Circle [constr] CenterX=0 CenterY=0 CenterZ=0 NormalX=0 NormalY=0 NormalZ=1 AngleXU=0 Radius=20
    g1: LineSegment [constr] StartX=-14.1421 StartY=14.1421 StartZ=0 EndX=14.1421 EndY=14.1421 EndZ=0
    g2: LineSegment [constr] StartX=14.1421 StartY=14.1421 StartZ=0 EndX=14.1421 EndY=-14.1421 EndZ=0
    g3: LineSegment [constr] StartX=14.1421 StartY=-14.1421 StartZ=0 EndX=-14.1421 EndY=-14.1421 EndZ=0
    g4: LineSegment [constr] StartX=-14.1421 StartY=-14.1421 StartZ=0 EndX=-14.1421 EndY=14.1421 EndZ=0
    g5: Circle CenterX=-14.1421 CenterY=14.1421 CenterZ=0 NormalX=0 NormalY=0 NormalZ=1 AngleXU=0 Radius=1.6
    g6: Circle CenterX=14.1421 CenterY=14.1421 CenterZ=0 NormalX=0 NormalY=0 NormalZ=1 AngleXU=0 Radius=1.6
    g7: Circle CenterX=14.1421 CenterY=-14.1421 CenterZ=0 NormalX=0 NormalY=0 NormalZ=1 AngleXU=0 Radius=1.6
    g8: Circle CenterX=-14.1421 CenterY=-14.1421 CenterZ=0 NormalX=0 NormalY=0 NormalZ=1 AngleXU=0 Radius=1.6
  constraints (22):
    c: Coincident(g0,g-1)
    c: Radius(g0) = 20
    c: Coincident(g1,g2)
    c: Coincident(g2,g3)
    c: Coincident(g3,g4)
    c: Coincident(g4,g1)
    c: Horizontal(g1)
    c: Horizontal(g3)
    c: Vertical(g2)
    c: Vertical(g4)
    c: PointOnObject(g1,g0)
    c: PointOnObject(g2,g0)
    c: PointOnObject(g1,g0)
    c: Equal(g1,g2)
    c: Coincident(g5,g1)
    c: Coincident(g6,g1)
    c: Coincident(g7,g2)
    c: Coincident(g8,g3)
    c: Equal(g8,g5)
    c: Equal(g5,g6)
    c: Equal(g6,g7)
    c: Radius(g6) = 1.6
FEATURE [PartDesign::Pocket] Pocket009  label="Screwholes Mounting"
  BaseFeature = -> Pad263
  Length = 12
  Length2 = 100
  Profile = -> Sketch590
  Type = 0
FEATURE [Sketcher::SketchObject] Sketch596
  MapMode = 5
  Placement = pos=(0,0,12) rot=(0,0,1;0rad)
  Support = -> [Pocket009]
  sketch-geometry (1):
    g0: Circle CenterX=0 CenterY=0 CenterZ=0 NormalX=0 NormalY=0 NormalZ=1 AngleXU=0 Radius=16.5
  constraints (2):
    c: Coincident(g0,g-1)
    c: Radius(g0) = 16.5
FEATURE [PartDesign::Pad] Pad264  label="M3 Nut Primitive051"
  Length = 1.2
  Length2 = 1.2
  Profile = -> Sketch651
  Type = 4
FEATURE [Sketcher::SketchObject] Sketch650
  ExternalGeometry = -> [Pad264]
  MapMode = 5
  Placement = pos=(0,0,0) rot=(0.57735,0.57735,0.57735;2.0944rad)
  Support = -> [YZ_Plane188]
  sketch-geometry (6):
    g0: LineSegment StartX=-2.67543 StartY=1.2 StartZ=0 EndX=-3.67543 EndY=1.2 EndZ=0
    g1: LineSegment StartX=-3.67543 StartY=1.2 StartZ=0 EndX=-3.67543 EndY=-1.2 EndZ=0
    g2: LineSegment StartX=-3.67543 StartY=-1.2 StartZ=0 EndX=-2.67543 EndY=-1.2 EndZ=0
    g3: LineSegment StartX=-2.67543 StartY=-1.2 StartZ=0 EndX=-3.17543 EndY=-1 EndZ=0
    g4: LineSegment StartX=-3.17543 StartY=-1 StartZ=0 EndX=-3.17543 EndY=1 EndZ=0
    g5: LineSegment StartX=-3.17543 StartY=1 StartZ=0 EndX=-2.67543 EndY=1.2 EndZ=0
  constraints (15):
    c: Horizontal(g0)
    c: Coincident(g0,g1)
    c: Coincident(g1,g2)
    c: Coincident(g2,g3)
    c: Coincident(g3,g4)
    c: Coincident(g4,g5)
    c: Coincident(g5,g0)
    c: Symmetric(g4,g3,g-1)
    c: Symmetric(g0,g2,g-1)
    c: Symmetric(g1,g0,g-1)
    c: DistanceX(g0,g4) = 0.5
    c: DistanceY(g3,g4) = 2
    c: DistanceY(g1,g0) = 2.4
    c: PointOnObject(g3,g-3)
    c: DistanceX(g4,g0) = 0.5
FEATURE [PartDesign::Groove] Groove053  label="M3 Nut Smooth051"
  Angle = 360
  Axis = (-2e-16,3e-16,1)
  Base = (0,0,0)
  BaseFeature = -> Pad264
  Profile = -> Sketch650
  ReferenceAxis = -> Sketch650 [V_Axis]
  Reversed = true
FEATURE [PartDesign::Chamfer] Chamfer119  label="M3 Nut Smooth Hole051"
  Base = -> Groove053 [Edge24,Edge23]
  BaseFeature = -> Groove053
  Size = 0.2
FEATURE [PartDesign::Body] Body136  label="M3 Nut024"
  Group = -> [Sketch651,Pad264,Sketch650,Groove053,Chamfer119]
  Origin = -> Origin198
  Placement = pos=(14.15,-14.15,3.5) rot=(0,0,1;0.261799rad)
  Tip = -> Chamfer119
FEATURE [App::Part] Part063  label="Shouldercap Nuts"
  Group = -> [Body134,Body137,Body136,Body130]
  Origin = -> Origin210
FEATURE [PartDesign::Pocket] Pocket014  label="Accesshole"
  BaseFeature = -> Pocket009
  Length = 7
  Length2 = 100
  Profile = -> Sketch596
  Type = 0
FEATURE [Sketcher::SketchObject] Sketch591
  MapMode = 5
  Placement = pos=(0,0,5) rot=(0,0,1;0rad)
  Support = -> [Pocket014]
  sketch-geometry (1):
    g0: Circle CenterX=0 CenterY=0 CenterZ=0 NormalX=0 NormalY=0 NormalZ=1 AngleXU=0 Radius=6.15
  constraints (2):
    c: Coincident(g0,g-1)
    c: Radius(g0) = 6.15
FEATURE [PartDesign::Pocket] Pocket010  label="Servohole"
  BaseFeature = -> Pocket014
  Length = 5
  Length2 = 100
  Profile = -> Sketch591
  Type = 0
FEATURE [Sketcher::SketchObject] Sketch597
  MapMode = 5
  Placement = pos=(0,0,5) rot=(0,0,1;0rad)
  Support = -> [Pocket010]
  sketch-geometry (32):
    g0: LineSegment [constr] StartX=3.75 StartY=6.49519 StartZ=0 EndX=-3.75 EndY=6.49519 EndZ=0
    g1: LineSegment [constr] StartX=-3.75 StartY=6.49519 StartZ=0 EndX=-7.5 EndY=9e-16 EndZ=0
    g2: LineSegment [constr] StartX=-7.5 StartY=9e-16 StartZ=0 EndX=-3.75 EndY=-6.49519 EndZ=0
    g3: LineSegment [constr] StartX=-3.75 StartY=-6.49519 StartZ=0 EndX=3.75 EndY=-6.49519 EndZ=0
    g4: LineSegment [constr] StartX=3.75 StartY=-6.49519 StartZ=0 EndX=7.5 EndY=0 EndZ=0
    g5: LineSegment [constr] StartX=7.5 StartY=0 StartZ=0 EndX=3.75 EndY=6.49519 EndZ=0
    g6: Circle [constr] CenterX=0 CenterY=0 CenterZ=0 NormalX=0 NormalY=0 NormalZ=1 AngleXU=0 Radius=7.5
    g7: LineSegment [constr] StartX=0 StartY=13.5 StartZ=0 EndX=-11.6913 EndY=6.75 EndZ=0
    g8: LineSegment [constr] StartX=-11.6913 StartY=6.75 StartZ=0 EndX=-11.6913 EndY=-6.75 EndZ=0
    g9: LineSegment [constr] StartX=-11.6913 StartY=-6.75 StartZ=0 EndX=0 EndY=-13.5 EndZ=0
    g10: LineSegment [constr] StartX=-5e-16 StartY=-13.5 StartZ=0 EndX=11.6913 EndY=-6.75 EndZ=0
    g11: LineSegment [constr] StartX=11.6913 StartY=-6.75 StartZ=0 EndX=11.6913 EndY=6.75 EndZ=0
    g12: LineSegment [constr] StartX=11.6913 StartY=6.75 StartZ=0 EndX=0 EndY=13.5 EndZ=0
    g13: Circle [constr] CenterX=0 CenterY=0 CenterZ=0 NormalX=0 NormalY=0 NormalZ=1 AngleXU=0 Radius=13.5
    g14: ArcOfCircle CenterX=0 CenterY=13.5 CenterZ=0 NormalX=0 NormalY=0 NormalZ=1 AngleXU=0 Radius=2.6 StartAngle=0.15815 EndAngle=2.98344
    g15: ArcOfCircle CenterX=11.6913 CenterY=6.75 CenterZ=0 NormalX=0 NormalY=0 NormalZ=1 AngleXU=0 Radius=2.6 StartAngle=5.39414 EndAngle=8.21943
    g16: ArcOfCircle CenterX=11.6913 CenterY=-6.75 CenterZ=0 NormalX=0 NormalY=0 NormalZ=1 AngleXU=0 Radius=2.6 StartAngle=4.34694 EndAngle=7.17223
    g17: ArcOfCircle CenterX=-5e-16 CenterY=-13.5 CenterZ=0 NormalX=0 NormalY=0 NormalZ=1 AngleXU=0 Radius=2.6 StartAngle=3.29974 EndAngle=6.12503
    g18: ArcOfCircle CenterX=-11.6913 CenterY=-6.75 CenterZ=0 NormalX=0 NormalY=0 NormalZ=1 AngleXU=0 Radius=2.6 StartAngle=2.25255 EndAngle=5.07784
    g19: ArcOfCircle CenterX=-11.6913 CenterY=6.75 CenterZ=0 NormalX=0 NormalY=0 NormalZ=1 AngleXU=0 Radius=2.6 StartAngle=1.20535 EndAngle=4.03064
    g20: LineSegment StartX=-2.56755 StartY=13.9095 StartZ=0 EndX=-3.75 EndY=6.49519 EndZ=0
    g21: LineSegment StartX=-3.75 StartY=6.49519 StartZ=0 EndX=-10.7622 EndY=9.17831 EndZ=0
    g22: LineSegment StartX=2.56755 StartY=13.9095 StartZ=0 EndX=3.75 EndY=6.49519 EndZ=0
    g23: LineSegment StartX=3.75 StartY=6.49519 StartZ=0 EndX=10.7622 EndY=9.17831 EndZ=0
    g24: LineSegment StartX=13.3297 StartY=4.73117 StartZ=0 EndX=7.5 EndY=0 EndZ=0
    g25: LineSegment StartX=7.5 StartY=0 StartZ=0 EndX=13.3297 EndY=-4.73117 EndZ=0
    g26: LineSegment StartX=10.7622 StartY=-9.17831 StartZ=0 EndX=3.75 EndY=-6.49519 EndZ=0
    g27: LineSegment StartX=3.75 StartY=-6.49519 StartZ=0 EndX=2.56755 EndY=-13.9095 EndZ=0
    g28: LineSegment StartX=-2.56755 StartY=-13.9095 StartZ=0 EndX=-3.75 EndY=-6.49519 EndZ=0
    g29: LineSegment StartX=-3.75 StartY=-6.49519 StartZ=0 EndX=-10.7622 EndY=-9.17831 EndZ=0
    g30: LineSegment StartX=-13.3297 StartY=-4.73117 StartZ=0 EndX=-7.5 EndY=9e-16 EndZ=0
    g31: LineSegment StartX=-7.5 StartY=9e-16 StartZ=0 EndX=-13.3297 EndY=4.73117 EndZ=0
  constraints (68):
    c: Coincident(g0,g1)
    c: Coincident(g1,g2)
    c: Coincident(g2,g3)
    c: Coincident(g3,g4)
    c: Coincident(g4,g5)
    c: Coincident(g5,g0)
    c: Equal(g0, g1-g5) x5
    c: PointOnObject(g0,g6)
    c: PointOnObject(g1,g6)
    c: PointOnObject(g2,g6)
    c: PointOnObject(g3,g6)
    c: PointOnObject(g4,g6)
    c: PointOnObject(g5,g6)
    c: Coincident(g6,g-1)
    c: Coincident(g7,g8)
    c: Coincident(g8,g9)
    c: Coincident(g9,g10)
    c: Coincident(g10,g11)
    c: Coincident(g11,g12)
    c: Coincident(g12,g7)
    c: Equal(g7, g8-g12) x5
    c: PointOnObject(g7,g13)
    c: PointOnObject(g8,g13)
    c: PointOnObject(g9,g13)
    c: PointOnObject(g10,g13)
    c: PointOnObject(g11,g13)
    c: PointOnObject(g12,g13)
    c: Coincident(g13,g-1)
    c: Horizontal(g0)
    c: Vertical(g8)
    c: Radius(g6) = 7.5
    c: Radius(g13) = 13.5
    c: Coincident(g14,g7)
    c: Coincident(g15,g11)
    c: Coincident(g16,g10)
    c: Coincident(g17,g9)
    c: Coincident(g18,g8)
    c: Coincident(g19,g7)
    c: Coincident(g20,g0)
    c: Coincident(g21,g20)
    c: Coincident(g22,g0)
    c: Coincident(g23,g22)
    c: Coincident(g24,g4)
    c: Coincident(g25,g24)
    c: Coincident(g26,g3)
    c: Coincident(g27,g26)
    c: Coincident(g28,g2)
    c: Coincident(g29,g28)
    c: Coincident(g31,g30)
    c: Tangent(g21,g19) = -1.5708
    c: Tangent(g20,g14) = -1.5708
    c: Tangent(g22,g14) = 1.5708
    c: Tangent(g23,g15) = 1.5708
    c: Tangent(g24,g15) = 1.5708
    c: Tangent(g25,g16) = 1.5708
    c: Tangent(g26,g16) = 1.5708
    c: Tangent(g27,g17) = 1.5708
    c: Tangent(g28,g17) = 1.5708
    c: Tangent(g29,g18) = 1.5708
    c: Tangent(g30,g18) = 1.5708
    c: Tangent(g31,g19) = 1.5708
    c: Radius(g14) = 2.6
    c: Equal(g14,g15)
    c: Equal(g15,g16)
    c: Equal(g16,g17)
    c: Equal(g17,g18)
    c: Equal(g18,g19)
    c: Coincident(g30,g1)
FEATURE [PartDesign::Pocket] Pocket012  label="Servohorn006"
  BaseFeature = -> Pocket010
  Length = 2
  Length2 = 100
  Profile = -> Sketch597
  Type = 0
FEATURE [PartDesign::Fillet] Fillet084  label="Smooth Servohorn Corners"
  Base = -> Pocket012 [Edge81,Edge87,Edge82,Edge88,Edge93,Edge94]
  BaseFeature = -> Pocket012
  Radius = 1
FEATURE [Sketcher::SketchObject] Sketch598
  MapMode = 5
  Placement = pos=(0,0,3) rot=(0,0,1;0rad)
  Support = -> [Fillet084]
  sketch-geometry (13):
    g0: LineSegment [constr] StartX=0 StartY=10.5 StartZ=0 EndX=-9.09327 EndY=5.25 EndZ=0
    g1: LineSegment [constr] StartX=-9.09327 StartY=5.25 StartZ=0 EndX=-9.09327 EndY=-5.25 EndZ=0
    g2: LineSegment [constr] StartX=-9.09327 StartY=-5.25 StartZ=0 EndX=0 EndY=-10.5 EndZ=0
    g3: LineSegment [constr] StartX=0 StartY=-10.5 StartZ=0 EndX=9.09327 EndY=-5.25 EndZ=0
    g4: LineSegment [constr] StartX=9.09327 StartY=-5.25 StartZ=0 EndX=9.09327 EndY=5.25 EndZ=0
    g5: LineSegment [constr] StartX=9.09327 StartY=5.25 StartZ=0 EndX=0 EndY=10.5 EndZ=0
    g6: Circle [constr] CenterX=0 CenterY=0 CenterZ=0 NormalX=0 NormalY=0 NormalZ=1 AngleXU=0 Radius=10.5
    g7: Circle CenterX=0 CenterY=10.5 CenterZ=0 NormalX=0 NormalY=0 NormalZ=1 AngleXU=0 Radius=0.95
    g8: Circle CenterX=9.09327 CenterY=5.25 CenterZ=0 NormalX=0 NormalY=0 NormalZ=1 AngleXU=0 Radius=0.95
    g9: Circle CenterX=9.09327 CenterY=-5.25 CenterZ=0 NormalX=0 NormalY=0 NormalZ=1 AngleXU=0 Radius=0.95
    g10: Circle CenterX=0 CenterY=-10.5 CenterZ=0 NormalX=0 NormalY=0 NormalZ=1 AngleXU=0 Radius=0.95
    g11: Circle CenterX=-9.09327 CenterY=-5.25 CenterZ=0 NormalX=0 NormalY=0 NormalZ=1 AngleXU=0 Radius=0.95
    g12: Circle CenterX=-9.09327 CenterY=5.25 CenterZ=0 NormalX=0 NormalY=0 NormalZ=1 AngleXU=0 Radius=0.95
  constraints (24):
    c: Coincident(g0,g1)
    c: Coincident(g1,g2)
    c: Coincident(g2,g3)
    c: Coincident(g3,g4)
    c: Coincident(g4,g5)
    c: Coincident(g5,g0)
    c: Equal(g0, g1-g5) x5
    c: PointOnObject(g0,g6)
    c: PointOnObject(g1,g6)
    c: PointOnObject(g2,g6)
    c: PointOnObject(g3,g6)
    c: PointOnObject(g4,g6)
    c: PointOnObject(g5,g6)
    c: Coincident(g6,g-1)
    c: PointOnObject(g5,g-2)
    c: Radius(g6) = 10.5
    c: Coincident(g7,g0)
    c: Coincident(g8,g4)
    c: Coincident(g9,g3)
    c: Coincident(g10,g2)
    c: Coincident(g11,g1)
    c: Coincident(g12,g0)
    c: Radius(g12) = 0.95
    c: Equal(g12, g7-g11) x5
FEATURE [PartDesign::Pocket] Pocket011  label="Screwholes Servohorn"
  BaseFeature = -> Fillet084
  Length = 3
  Length2 = 100
  Profile = -> Sketch598
  Type = 0
FEATURE [Sketcher::SketchObject] Sketch592
  MapMode = 5
  Placement = pos=(0,0,0) rot=(1,0,0;3.14159rad)
  Support = -> [Pocket011]
  sketch-geometry (10):
    g0: Circle [constr] CenterX=0 CenterY=0 CenterZ=0 NormalX=0 NormalY=0 NormalZ=1 AngleXU=0 Radius=20
    g1: LineSegment [constr] StartX=-14.1421 StartY=14.1421 StartZ=0 EndX=14.1421 EndY=14.1421 EndZ=0
    g2: LineSegment [constr] StartX=14.1421 StartY=14.1421 StartZ=0 EndX=14.1421 EndY=-14.1421 EndZ=0
    g3: LineSegment [constr] StartX=14.1421 StartY=-14.1421 StartZ=0 EndX=-14.1421 EndY=-14.1421 EndZ=0
    g4: LineSegment [constr] StartX=-14.1421 StartY=-14.1421 StartZ=0 EndX=-14.1421 EndY=14.1421 EndZ=0
    g5: Circle CenterX=-14.1421 CenterY=14.1421 CenterZ=0 NormalX=0 NormalY=0 NormalZ=1 AngleXU=0 Radius=1.2e-15
    g6: Circle CenterX=14.1421 CenterY=14.1421 CenterZ=0 NormalX=0 NormalY=0 NormalZ=1 AngleXU=0 Radius=2.85
    g7: Circle CenterX=14.1421 CenterY=-14.1421 CenterZ=0 NormalX=0 NormalY=0 NormalZ=1 AngleXU=0 Radius=2.85
    g8: Circle CenterX=-14.1421 CenterY=14.1421 CenterZ=0 NormalX=0 NormalY=0 NormalZ=1 AngleXU=0 Radius=2.85
    g9: Circle CenterX=-14.1421 CenterY=-14.1421 CenterZ=0 NormalX=0 NormalY=0 NormalZ=1 AngleXU=0 Radius=2.85
  constraints (24):
    c: Coincident(g0,g-1)
    c: Radius(g0) = 20
    c: Coincident(g1,g2)
    c: Coincident(g2,g3)
    c: Coincident(g3,g4)
    c: Coincident(g4,g1)
    c: Horizontal(g1)
    c: Horizontal(g3)
    c: Vertical(g2)
    c: Vertical(g4)
    c: PointOnObject(g1,g0)
    c: PointOnObject(g2,g0)
    c: PointOnObject(g1,g0)
    c: Equal(g1,g2)
    c: Coincident(g5,g1)
    c: Tangent(g5,g0)
    c: Coincident(g6,g1)
    c: Coincident(g7,g2)
    c: Coincident(g8,g5)
    c: Coincident(g9,g3)
    c: Equal(g9,g8)
    c: Equal(g8,g6)
    c: Equal(g6,g7)
    c: Radius(g6) = 2.85
FEATURE [PartDesign::Pocket] Pocket013  label="Screwheads Mounting"
  BaseFeature = -> Pocket011
  Length = 8
  Length2 = 100
  Profile = -> Sketch592
  Type = 0
FEATURE [PartDesign::Chamfer] Chamfer118  label="Screwheads Bottom Chamfer"
  Base = -> Pocket013 [Edge140,Edge139,Edge138,Edge137]
  BaseFeature = -> Pocket013
  Size = 1.2
FEATURE [PartDesign::Body] Body002  label="Shoulder_Joint_Servohorn_Cap"
  Group = -> [Sketch593,Pad263,Sketch590,Pocket009,Sketch596,Pocket014,Sketch591,Pocket010,Sketch597,Pocket012,Fillet084,Sketch598,Pocket011,Sketch592,Pocket013,Chamfer118]
  Origin = -> Origin002
  Tip = -> Chamfer118
FEATURE [Sketcher::SketchObject] Sketch664
  MapMode = 5
  Support = -> [XY_Plane220]
  sketch-geometry (1):
    g0: Circle CenterX=0 CenterY=0 CenterZ=0 NormalX=0 NormalY=0 NormalZ=1 AngleXU=0 Radius=2.75
  constraints (2):
    c: Coincident(g0,g-1)
    c: Radius(g0) = 2.75
FEATURE [PartDesign::Pad] Pad266  label="M3x8 Head034"
  Length = 3
  Length2 = 100
  Profile = -> Sketch664
  Type = 0
FEATURE [Sketcher::SketchObject] Sketch666
  MapMode = 5
  Placement = pos=(0,0,3) rot=(0,0,1;0rad)
  Support = -> [Pad266]
  sketch-geometry (1):
    g0: Circle CenterX=0 CenterY=0 CenterZ=0 NormalX=0 NormalY=0 NormalZ=1 AngleXU=0 Radius=1.5
  constraints (2):
    c: Coincident(g0,g-1)
    c: Radius(g0) = 1.5
FEATURE [PartDesign::Pad] Pad265  label="M3x8 Thread034"
  BaseFeature = -> Pad266
  Length = 8
  Length2 = 100
  Profile = -> Sketch666
  Type = 0
FEATURE [Sketcher::SketchObject] Sketch665
  MapMode = 5
  Placement = pos=(0,0,0) rot=(1,0,0;3.14159rad)
  Support = -> [Pad265]
  sketch-geometry (7):
    g0: LineSegment StartX=1.275 StartY=0.736122 StartZ=0 EndX=0 EndY=1.47224 EndZ=0
    g1: LineSegment StartX=0 StartY=1.47224 StartZ=0 EndX=-1.275 EndY=0.736122 EndZ=0
    g2: LineSegment StartX=-1.275 StartY=0.736122 StartZ=0 EndX=-1.275 EndY=-0.736122 EndZ=0
    g3: LineSegment StartX=-1.275 StartY=-0.736122 StartZ=0 EndX=1.34766e-11 EndY=-1.47224 EndZ=0
    g4: LineSegment StartX=1.34766e-11 StartY=-1.47224 StartZ=0 EndX=1.275 EndY=-0.736122 EndZ=0
    g5: LineSegment StartX=1.275 StartY=-0.736122 StartZ=0 EndX=1.275 EndY=0.736122 EndZ=0
    g6: Circle [constr] CenterX=0 CenterY=0 CenterZ=0 NormalX=0 NormalY=0 NormalZ=1 AngleXU=0 Radius=1.47224
  constraints (16):
    c: Coincident(g0,g1)
    c: Coincident(g1,g2)
    c: Coincident(g2,g3)
    c: Coincident(g3,g4)
    c: Coincident(g4,g5)
    c: Coincident(g5,g0)
    c: Equal(g0, g1-g5) x5
    c: PointOnObject(g0,g6)
    c: PointOnObject(g1,g6)
    c: PointOnObject(g2,g6)
    c: PointOnObject(g3,g6)
    c: PointOnObject(g4,g6)
    c: PointOnObject(g5,g6)
    c: Coincident(g6,g-1)
    c: PointOnObject(g0,g-2)
    c: DistanceX(g1,g0) = 2.55
FEATURE [PartDesign::Pocket] Pocket273  label="M3x8 Wrench034"
  BaseFeature = -> Pad265
  Length = 1.3
  Length2 = 100
  Profile = -> Sketch665
  Type = 0
FEATURE [PartDesign::Chamfer] Chamfer120  label="M3x8 Smooth034"
  Base = -> Pocket273 [Face11,Edge2,Edge24,Edge3]
  BaseFeature = -> Pocket273
  Size = 0.2
FEATURE [Sketcher::SketchObject] Sketch667
  MapMode = 5
  Placement = pos=(0,0,0) rot=(0.57735,0.57735,0.57735;2.0944rad)
  Support = -> [YZ_Plane220]
  sketch-geometry (1):
    g0: LineSegment StartX=0 StartY=0 StartZ=0 EndX=0 EndY=190 EndZ=0
  constraints (3):
    c: Coincident(g0,g-1)
    c: Vertical(g0)
    c: DistanceY(g0,g0) = 190
FEATURE [PartDesign::Body] Body153  label="M3x035"
  Group = -> [Sketch664,Pad266,Sketch666,Pad265,Sketch665,Pocket273,Chamfer120,Sketch667]
  Origin = -> Origin220
  Placement = pos=(-5.2,-40,200.6) rot=(-1,0,0;1.5708rad)
  Tip = -> Chamfer120
FEATURE [Sketcher::SketchObject] Sketch668
  ExternalGeometry = -> [Fillet083]
  MapMode = 5
  Support = -> [XY_Plane198]
  sketch-geometry (3):
    g0: ArcOfCircle [constr] CenterX=-2e-16 CenterY=-3e-16 CenterZ=0 NormalX=0 NormalY=0 NormalZ=1 AngleXU=0 Radius=13.5 StartAngle=3.66519 EndAngle=5.75959
    g1: ArcOfCircle [constr] CenterX=-2e-16 CenterY=-3e-16 CenterZ=0 NormalX=0 NormalY=0 NormalZ=1 AngleXU=0 Radius=13.5 StartAngle=2.61799 EndAngle=3.66519
    g2: LineSegment StartX=-11.6913 StartY=-6.75 StartZ=0 EndX=11.6913 EndY=6.75 EndZ=0
  constraints (9):
    c: Coincident(g0,g-5)
    c: Coincident(g0,g-4)
    c: Coincident(g1,g0)
    c: Coincident(g1,g0)
    c: Angle(g0) = 2.0944
    c: Angle(g1) = 1.0472
    c: Coincident(g1,g-3)
    c: Coincident(g2,g0)
    c: Coincident(g2,g-6)
FEATURE [PartDesign::Body] Body150  label="Futuba FSH6B003"
  Group = -> [Sketch595,Pad237,Sketch589,Pocket257,Sketch580,Pocket260,Sketch579,Pocket256,Sketch594,Pad236,Fillet083,Sketch668]
  Origin = -> Origin194
  Tip = -> Fillet083
FEATURE [App::Part] Part054  label="Servphorn"
  Group = -> [Body150]
  Origin = -> Origin190
  Placement = pos=(0,0,3.45) rot=(0,0,1;0rad)
FEATURE [App::Part] Part053  label="Shoulderjoint CAP"
  Group = -> [Part056,Part054,Body002]
  Origin = -> Origin185
  Placement = pos=(0,0,-12) rot=(0,0,1;0rad)
FEATURE [App::Part] Part052  label="FL Shoulder Joint"
  Group = -> [Body001,Part053,Part059,Part063,Part051,Body153]
  Origin = -> Origin197
  Placement = pos=(-5.2,-45.6,200.6) rot=(1,0,0;1.5708rad)
FEATURE [Sketcher::SketchObject] Sketch679
  MapMode = 5
  Placement = pos=(0,0,0) rot=(1,0,0;1.5708rad)
  Support = -> [XZ_Plane221]
  sketch-geometry (1):
    g0: Circle CenterX=1.55 CenterY=4 CenterZ=0 NormalX=0 NormalY=0 NormalZ=1 AngleXU=0 Radius=0.75
  constraints (3):
    c: Radius(g0) = 0.75
    c: DistanceY(g-1,g0) = 4
    c: DistanceX(g-1,g0) = 1.55
FEATURE [Sketcher::SketchObject] Sketch685
  MapMode = 5
  Support = -> [XY_Plane221]
  sketch-geometry (4):
    g0: LineSegment StartX=-10 StartY=20.15 StartZ=0 EndX=10 EndY=20.15 EndZ=0
    g1: LineSegment StartX=10 StartY=20.15 StartZ=0 EndX=10 EndY=-20.15 EndZ=0
    g2: LineSegment StartX=10 StartY=-20.15 StartZ=0 EndX=-10 EndY=-20.15 EndZ=0
    g3: LineSegment StartX=-10 StartY=-20.15 StartZ=0 EndX=-10 EndY=20.15 EndZ=0
  constraints (10):
    c: Coincident(g0,g1)
    c: Coincident(g1,g2)
    c: Coincident(g2,g3)
    c: Coincident(g3,g0)
    c: Horizontal(g2)
    c: Vertical(g3)
    c: DistanceX(g0,g0) = 20
    c: DistanceY(g1,g1) = 40.3
    c: Symmetric(g0,g1,g-1)
    c: Symmetric(g0,g0,g-2)
FEATURE [Sketcher::SketchObject] Sketch686
  MapMode = 5
  Placement = pos=(0,0,0) rot=(1,0,0;1.5708rad)
  Support = -> [XZ_Plane223]
  sketch-geometry (1):
    g0: Circle CenterX=-1.55 CenterY=4 CenterZ=0 NormalX=0 NormalY=0 NormalZ=1 AngleXU=0 Radius=0.75
  constraints (3):
    c: Radius(g0) = 0.75
    c: DistanceY(g-1,g0) = 4
    c: DistanceX(g0,g-1) = 1.55
FEATURE [PartDesign::Pad] Pad269
  Length = 10
  Length2 = 100
  Placement = pos=(0,0,0) rot=(1,0,0;1.5708rad)
  Profile = -> Sketch686
  Reversed = true
  Type = 0
FEATURE [Sketcher::SketchObject] Sketch687
  MapMode = 5
  Placement = pos=(0,0,0) rot=(1,0,0;1.5708rad)
  Support = -> [XZ_Plane225]
  sketch-geometry (1):
    g0: Circle CenterX=0 CenterY=4 CenterZ=0 NormalX=0 NormalY=0 NormalZ=1 AngleXU=0 Radius=0.75
  constraints (3):
    c: PointOnObject(g0,g-2)
    c: Radius(g0) = 0.75
    c: DistanceY(g-1,g0) = 4
FEATURE [Sketcher::SketchObject] Sketch688
  MapMode = 5
  Support = -> [XY_Plane222]
  sketch-geometry (1):
    g0: Circle CenterX=0 CenterY=10.15 CenterZ=0 NormalX=0 NormalY=0 NormalZ=1 AngleXU=0 Radius=3
  constraints (3):
    c: PointOnObject(g0,g-2)
    c: DistanceY(g-1,g0) = 10.15
    c: Radius(g0) = 3
FEATURE [PartDesign::Pad] Pad270
  Length = 5
  Length2 = 100
  Profile = -> Sketch688
  Type = 0
FEATURE [Sketcher::SketchObject] Sketch682
  ExternalGeometry = -> [Pad270]
  MapMode = 5
  Placement = pos=(0,0,5) rot=(0,0,1;0rad)
  Support = -> [Pad270]
  sketch-geometry (1):
    g0: Circle CenterX=0 CenterY=10.15 CenterZ=0 NormalX=0 NormalY=0 NormalZ=1 AngleXU=0 Radius=1.5
  constraints (2):
    c: Coincident(g0,g-3)
    c: Radius(g0) = 1.5
FEATURE [PartDesign::Pocket] Pocket277
  BaseFeature = -> Pad270
  Length = 4
  Length2 = 100
  Profile = -> Sketch682
  Type = 0
FEATURE [PartDesign::Chamfer] Chamfer121
  Base = -> Pocket277 [Edge3]
  BaseFeature = -> Pocket277
  Size = 0.25
FEATURE [PartDesign::Body] Body155  label="orange wire005"
  Group = -> [Sketch686,Pad269]
  Origin = -> Origin224
  Placement = pos=(0,25.15,0) rot=(0,0,1;0rad)
  Tip = -> Pad269
FEATURE [PartDesign::Body] Body158  label="Gear005"
  Group = -> [Sketch688,Pad270,Sketch682,Pocket277,Chamfer121]
  Origin = -> Origin225
  Placement = pos=(0,0,38.25) rot=(0,0,1;0rad)
  Tip = -> Chamfer121
FEATURE [PartDesign::Pad] Pad276  label="Baseblock005"
  Length = 26.6
  Length2 = 100
  Profile = -> Sketch685
  Type = 0
FEATURE [Sketcher::SketchObject] Sketch673
  MapMode = 5
  Placement = pos=(0,0,26.6) rot=(0,0,1;0rad)
  Support = -> [Pad276]
  sketch-geometry (4):
    g0: LineSegment StartX=-10 StartY=-26.8 StartZ=0 EndX=10 EndY=-26.8 EndZ=0
    g1: LineSegment StartX=10 StartY=-26.8 StartZ=0 EndX=10 EndY=26.8 EndZ=0
    g2: LineSegment StartX=10 StartY=26.8 StartZ=0 EndX=-10 EndY=26.8 EndZ=0
    g3: LineSegment StartX=-10 StartY=26.8 StartZ=0 EndX=-10 EndY=-26.8 EndZ=0
  constraints (10):
    c: Coincident(g0,g1)
    c: Coincident(g1,g2)
    c: Coincident(g2,g3)
    c: Coincident(g3,g0)
    c: Horizontal(g0)
    c: Vertical(g3)
    c: Symmetric(g1,g2,g-2)
    c: Symmetric(g1,g0,g-1)
    c: DistanceX(g2,g2) = 20
    c: DistanceY(g1,g1) = 53.6
FEATURE [PartDesign::Pad] Pad274
  BaseFeature = -> Pad276
  Length = 2.5
  Length2 = 100
  Profile = -> Sketch673
  Type = 0
FEATURE [Sketcher::SketchObject] Sketch671
  MapMode = 5
  Placement = pos=(0,0,29.1) rot=(0,0,1;0rad)
  Support = -> [Pad274]
  sketch-geometry (4):
    g0: LineSegment StartX=-10 StartY=-20.15 StartZ=0 EndX=10 EndY=-20.15 EndZ=0
    g1: LineSegment StartX=10 StartY=-20.15 StartZ=0 EndX=10 EndY=20.15 EndZ=0
    g2: LineSegment StartX=10 StartY=20.15 StartZ=0 EndX=-10 EndY=20.15 EndZ=0
    g3: LineSegment StartX=-10 StartY=20.15 StartZ=0 EndX=-10 EndY=-20.15 EndZ=0
  constraints (10):
    c: Coincident(g0,g1)
    c: Coincident(g1,g2)
    c: Coincident(g2,g3)
    c: Coincident(g3,g0)
    c: Horizontal(g0)
    c: Vertical(g3)
    c: Symmetric(g1,g2,g-2)
    c: Symmetric(g1,g0,g-1)
    c: DistanceX(g2,g2) = 20
    c: DistanceY(g1,g1) = 40.3
FEATURE [PartDesign::Pad] Pad277
  Length = 10
  Length2 = 100
  Placement = pos=(0,0,0) rot=(1,0,0;1.5708rad)
  Profile = -> Sketch679
  Reversed = true
  Type = 0
FEATURE [PartDesign::Body] Body156  label="brown wire005"
  Group = -> [Sketch679,Pad277]
  Origin = -> Origin222
  Placement = pos=(0,25.15,0) rot=(0,0,1;0rad)
  Tip = -> Pad277
FEATURE [PartDesign::Pad] Pad278
  Length = 10
  Length2 = 100
  Placement = pos=(0,0,0) rot=(1,0,0;1.5708rad)
  Profile = -> Sketch687
  Reversed = true
  Type = 0
FEATURE [PartDesign::Body] Body157  label="red wire005"
  Group = -> [Sketch687,Pad278]
  Origin = -> Origin221
  Placement = pos=(0,25.15,0) rot=(0,0,1;0rad)
  Tip = -> Pad278
FEATURE [PartDesign::Pad] Pad279
  BaseFeature = -> Pad274
  Length = 6
  Length2 = 100
  Profile = -> Sketch671
  Type = 0
FEATURE [Sketcher::SketchObject] Sketch678
  ExternalGeometry = -> [Pad279]
  MapMode = 5
  Placement = pos=(0,0,35.1) rot=(0,0,1;0rad)
  Support = -> [Pad279]
  sketch-geometry (7):
    g0: ArcOfCircle CenterX=-3e-16 CenterY=10.15 CenterZ=0 NormalX=0 NormalY=0 NormalZ=1 AngleXU=0 Radius=9.5 StartAngle=5.9573 EndAngle=9.75066
    g1: LineSegment StartX=-9 StartY=7.10862 StartZ=0 EndX=-9 EndY=-14.15 EndZ=0
    g2: LineSegment StartX=-9 StartY=-14.15 StartZ=0 EndX=-5 EndY=-14.15 EndZ=0
    g3: LineSegment StartX=5 StartY=-14.15 StartZ=0 EndX=9 EndY=-14.15 EndZ=0
    g4: LineSegment StartX=9 StartY=-14.15 StartZ=0 EndX=9 EndY=7.10862 EndZ=0
    g5: ArcOfCircle CenterX=-3e-16 CenterY=-10.4 CenterZ=0 NormalX=0 NormalY=0 NormalZ=1 AngleXU=0 Radius=6.25 StartAngle=3.78509 EndAngle=5.63968
    g6: LineSegment [constr] StartX=0 StartY=-20.15 StartZ=0 EndX=0 EndY=-16.65 EndZ=0
  constraints (22):
    c: Symmetric(g0,g0,g-2)
    c: Coincident(g1,g0)
    c: Vertical(g1)
    c: Coincident(g2,g1)
    c: Horizontal(g2)
    c: Horizontal(g3)
    c: Coincident(g4,g3)
    c: Coincident(g4,g0)
    c: Vertical(g4)
    c: Symmetric(g2,g3,g-2)
    c: Coincident(g5,g2)
    c: Coincident(g5,g3)
    c: DistanceY(g-3,g3) = 6
    c: DistanceY(g0,g-4) = 10
    c: Radius(g0) = 9.5
    c: DistanceX(g0,g0) = 18
    c: PointOnObject(g6,g-3)
    c: PointOnObject(g6,g5)
    c: Vertical(g6)
    c: DistanceY(g6,g6) = 3.5
    c: DistanceX(g2,g3) = 10
    c: PointOnObject(g6,g-2)
FEATURE [PartDesign::Pad] Pad272
  BaseFeature = -> Pad279
  Length = 2.5
  Length2 = 100
  Profile = -> Sketch678
  Type = 0
FEATURE [Sketcher::SketchObject] Sketch680
  ExternalGeometry = -> [Pad272]
  MapMode = 5
  Placement = pos=(0,0,37.6) rot=(0,0,1;0rad)
  Support = -> [Pad272]
  sketch-geometry (1):
    g0: Circle CenterX=-3e-16 CenterY=10.15 CenterZ=0 NormalX=0 NormalY=0 NormalZ=1 AngleXU=0 Radius=6.5
  constraints (2):
    c: Coincident(g0,g-3)
    c: Radius(g0) = 6.5
FEATURE [PartDesign::Pad] Pad280
  BaseFeature = -> Pad272
  Length = 1
  Length2 = 100
  Profile = -> Sketch680
  Type = 0
FEATURE [Sketcher::SketchObject] Sketch672
  ExternalGeometry = -> [Pad280]
  MapMode = 5
  Placement = pos=(0,0,38.6) rot=(0,0,1;0rad)
  Support = -> [Pad280]
  sketch-geometry (1):
    g0: Circle CenterX=0 CenterY=10.15 CenterZ=0 NormalX=0 NormalY=0 NormalZ=1 AngleXU=0 Radius=5.5
  constraints (2):
    c: Coincident(g0,g-3)
    c: Radius(g0) = 5.5
FEATURE [PartDesign::Pad] Pad271
  BaseFeature = -> Pad280
  Length = 0.5
  Length2 = 100
  Profile = -> Sketch672
  Type = 0
FEATURE [Sketcher::SketchObject] Sketch684
  ExternalGeometry = -> [Pad271]
  MapMode = 5
  Placement = pos=(0,0,39.1) rot=(0,0,1;0rad)
  Support = -> [Pad271]
  sketch-geometry (1):
    g0: Circle CenterX=0 CenterY=10.15 CenterZ=0 NormalX=0 NormalY=0 NormalZ=1 AngleXU=0 Radius=3
  constraints (2):
    c: Coincident(g0,g-3)
    c: Radius(g0) = 3
FEATURE [PartDesign::Pad] Pad281
  BaseFeature = -> Pad271
  Length = 4
  Length2 = 100
  Profile = -> Sketch684
  Type = 0
FEATURE [Sketcher::SketchObject] Sketch676
  ExternalGeometry = -> [Pad281]
  MapMode = 5
  Placement = pos=(0,0,43.1) rot=(0,0,1;0rad)
  Support = -> [Pad281]
  sketch-geometry (1):
    g0: Circle CenterX=0 CenterY=10.15 CenterZ=0 NormalX=0 NormalY=0 NormalZ=1 AngleXU=0 Radius=1.5
  constraints (2):
    c: Coincident(g0,g-3)
    c: Radius(g0) = 1.5
FEATURE [PartDesign::Pocket] Pocket276
  BaseFeature = -> Pad281
  Length = 5
  Length2 = 100
  Profile = -> Sketch676
  Type = 0
FEATURE [Sketcher::SketchObject] Sketch670
  MapMode = 5
  Placement = pos=(0,0,29.1) rot=(0,0,1;0rad)
  Support = -> [Pocket276]
  sketch-geometry (4):
    g0: Circle CenterX=-4.91157 CenterY=25.3 CenterZ=0 NormalX=0 NormalY=0 NormalZ=1 AngleXU=0 Radius=2.25
    g1: Circle CenterX=4.91157 CenterY=25.3 CenterZ=0 NormalX=0 NormalY=0 NormalZ=1 AngleXU=0 Radius=2.25
    g2: Circle CenterX=-4.91157 CenterY=-25.3 CenterZ=0 NormalX=0 NormalY=0 NormalZ=1 AngleXU=0 Radius=2.25
    g3: Circle CenterX=4.91157 CenterY=-25.3 CenterZ=0 NormalX=0 NormalY=0 NormalZ=1 AngleXU=0 Radius=2.25
  constraints (8):
    c: Equal(g3,g2)
    c: Equal(g2,g1)
    c: Equal(g1,g0)
    c: Radius(g1) = 2.25
    c: Symmetric(g1,g0,g-2)
    c: Symmetric(g3,g2,g-2)
    c: Symmetric(g3,g1,g-1)
    c: DistanceY(g3,g1) = 50.6
FEATURE [PartDesign::Pocket] Pocket275
  BaseFeature = -> Pocket276
  Length = 5
  Length2 = 100
  Profile = -> Sketch670
  Type = 0
FEATURE [Sketcher::SketchObject] Sketch683
  MapMode = 5
  Placement = pos=(0,0,29.1) rot=(0,0,1;0rad)
  Support = -> [Pocket275]
  sketch-geometry (8):
    g0: LineSegment StartX=-0.5 StartY=26.8 StartZ=0 EndX=0.5 EndY=26.8 EndZ=0
    g1: LineSegment StartX=0.5 StartY=26.8 StartZ=0 EndX=0.5 EndY=20.15 EndZ=0
    g2: LineSegment StartX=0.5 StartY=20.15 StartZ=0 EndX=-0.5 EndY=20.15 EndZ=0
    g3: LineSegment StartX=-0.5 StartY=20.15 StartZ=0 EndX=-0.5 EndY=26.8 EndZ=0
    g4: LineSegment StartX=-0.5 StartY=-20.15 StartZ=0 EndX=0.5 EndY=-20.15 EndZ=0
    g5: LineSegment StartX=0.5 StartY=-20.15 StartZ=0 EndX=0.5 EndY=-26.8 EndZ=0
    g6: LineSegment StartX=0.5 StartY=-26.8 StartZ=0 EndX=-0.5 EndY=-26.8 EndZ=0
    g7: LineSegment StartX=-0.5 StartY=-26.8 StartZ=0 EndX=-0.5 EndY=-20.15 EndZ=0
  constraints (20):
    c: Coincident(g0,g1)
    c: Coincident(g1,g2)
    c: Coincident(g2,g3)
    c: Coincident(g3,g0)
    c: Horizontal(g2)
    c: Vertical(g1)
    c: Vertical(g3)
    c: Coincident(g4,g5)
    c: Coincident(g5,g6)
    c: Coincident(g6,g7)
    c: Coincident(g7,g4)
    c: Horizontal(g6)
    c: Vertical(g7)
    c: Symmetric(g4,g4,g-2)
    c: Symmetric(g0,g0,g-2)
    c: Symmetric(g0,g5,g-1)
    c: DistanceY(g5,g0) = 53.6
    c: DistanceY(g4,g1) = 40.3
    c: DistanceX(g0,g0) = 1
    c: Symmetric(g4,g1,g-1)
FEATURE [PartDesign::Pad] Pad268
  BaseFeature = -> Pocket275
  Length = 2
  Length2 = 100
  Profile = -> Sketch683
  Type = 0
FEATURE [Sketcher::SketchObject] Sketch674
  ExternalGeometry = -> [Pad268]
  MapMode = 5
  Placement = pos=(0.5,0,0) rot=(0.57735,0.57735,0.57735;2.0944rad)
  Support = -> [Pad268]
  sketch-geometry (6):
    g0: LineSegment StartX=-26.8 StartY=29.1 StartZ=0 EndX=-26.8 EndY=31.1 EndZ=0
    g1: LineSegment StartX=-26.8 StartY=31.1 StartZ=0 EndX=-20.15 EndY=31.1 EndZ=0
    g2: LineSegment StartX=-20.15 StartY=31.1 StartZ=0 EndX=-26.8 EndY=29.1 EndZ=0
    g3: LineSegment StartX=20.15 StartY=31.1 StartZ=0 EndX=26.8 EndY=31.1 EndZ=0
    g4: LineSegment StartX=26.8 StartY=31.1 StartZ=0 EndX=26.8 EndY=29.1 EndZ=0
    g5: LineSegment StartX=26.8 StartY=29.1 StartZ=0 EndX=20.15 EndY=31.1 EndZ=0
  constraints (14):
    c: Vertical(g0)
    c: Coincident(g0,g1)
    c: Horizontal(g1)
    c: Coincident(g1,g2)
    c: Coincident(g2,g0)
    c: Coincident(g3,g4)
    c: Coincident(g4,g5)
    c: Coincident(g5,g3)
    c: Symmetric(g0,g4,g-2)
    c: Symmetric(g3,g0,g-2)
    c: Symmetric(g1,g3,g-2)
    c: DistanceX(g0,g3) = 53.6
    c: DistanceY(g4,g4) = 2
    c: Coincident(g3,g-3)
FEATURE [PartDesign::Pocket] Pocket274
  BaseFeature = -> Pad268
  Length = 1
  Length2 = 100
  Profile = -> Sketch674
  Type = 0
FEATURE [PartDesign::Fillet] Fillet086
  Base = -> Pocket274 [Edge26,Edge27,Edge72,Edge63,Edge70,Edge78,Edge51,Edge49,Edge71,Edge50,Edge79,Edge86,Edge30,Edge21,Edge4,Edge29,Edge105,Edge107,Edge109,Edge111,Edge113,Edge114,Edge123]
  BaseFeature = -> Pocket274
  Radius = 0.4
FEATURE [Sketcher::SketchObject] Sketch677
  MapMode = 5
  Placement = pos=(0,20.15,0) rot=(0,0.707107,0.707107;3.14159rad)
  Support = -> [Fillet086]
  sketch-geometry (4):
    g0: LineSegment StartX=-3.25 StartY=2 StartZ=0 EndX=3.25 EndY=2 EndZ=0
    g1: LineSegment StartX=3.25 StartY=2 StartZ=0 EndX=3.25 EndY=6 EndZ=0
    g2: LineSegment StartX=3.25 StartY=6 StartZ=0 EndX=-3.25 EndY=6 EndZ=0
    g3: LineSegment StartX=-3.25 StartY=6 StartZ=0 EndX=-3.25 EndY=2 EndZ=0
  constraints (11):
    c: Coincident(g0,g1)
    c: Coincident(g1,g2)
    c: Coincident(g2,g3)
    c: Coincident(g3,g0)
    c: Horizontal(g0)
    c: Vertical(g1)
    c: Vertical(g3)
    c: DistanceY(g-1,g0) = 2
    c: DistanceY(g1,g1) = 4
    c: Symmetric(g2,g1,g-2)
    c: DistanceX(g2,g2) = 6.5
FEATURE [PartDesign::Pad] Pad275
  BaseFeature = -> Fillet086
  Length = 1
  Length2 = 100
  Profile = -> Sketch677
  Type = 0
FEATURE [Sketcher::SketchObject] Sketch675
  MapMode = 5
  Placement = pos=(0,21.15,0) rot=(0,0.707107,0.707107;3.14159rad)
  Support = -> [Pad275]
  sketch-geometry (4):
    g0: LineSegment StartX=-2.75 StartY=5.5 StartZ=0 EndX=2.75 EndY=5.5 EndZ=0
    g1: LineSegment StartX=2.75 StartY=5.5 StartZ=0 EndX=2.75 EndY=2.5 EndZ=0
    g2: LineSegment StartX=2.75 StartY=2.5 StartZ=0 EndX=-2.75 EndY=2.5 EndZ=0
    g3: LineSegment StartX=-2.75 StartY=2.5 StartZ=0 EndX=-2.75 EndY=5.5 EndZ=0
  constraints (11):
    c: Coincident(g0,g1)
    c: Coincident(g1,g2)
    c: Coincident(g2,g3)
    c: Coincident(g3,g0)
    c: Horizontal(g0)
    c: Vertical(g1)
    c: Vertical(g3)
    c: Symmetric(g1,g2,g-2)
    c: DistanceY(g1,g0) = 3
    c: DistanceY(g-1,g1) = 2.5
    c: DistanceX(g0,g0) = 5.5
FEATURE [PartDesign::Pad] Pad267
  BaseFeature = -> Pad275
  Length = 4
  Length2 = 100
  Profile = -> Sketch675
  Type = 0
FEATURE [Sketcher::SketchObject] Sketch681
  MapMode = 5
  Placement = pos=(0,0,0) rot=(1,0,0;3.14159rad)
  Support = -> [Pad267]
  sketch-geometry (4):
    g0: LineSegment StartX=-10 StartY=-20.15 StartZ=0 EndX=10 EndY=-20.15 EndZ=0
    g1: LineSegment StartX=10 StartY=-20.15 StartZ=0 EndX=10 EndY=20.15 EndZ=0
    g2: LineSegment StartX=10 StartY=20.15 StartZ=0 EndX=-10 EndY=20.15 EndZ=0
    g3: LineSegment StartX=-10 StartY=20.15 StartZ=0 EndX=-10 EndY=-20.15 EndZ=0
  constraints (10):
    c: Coincident(g0,g1)
    c: Coincident(g1,g2)
    c: Coincident(g2,g3)
    c: Coincident(g3,g0)
    c: Horizontal(g0)
    c: Vertical(g1)
    c: Symmetric(g2,g1,g-2)
    c: Symmetric(g0,g2,g-1)
    c: DistanceX(g2,g2) = 20
    c: DistanceY(g1,g1) = 40.3
FEATURE [PartDesign::Pad] Pad273
  BaseFeature = -> Pad267
  Length = 2
  Length2 = 100
  Profile = -> Sketch681
  Type = 0
FEATURE [PartDesign::Chamfer] Chamfer122
  Base = -> Pad273 [Face7]
  BaseFeature = -> Pad273
  Size = 1.5
FEATURE [PartDesign::Fillet] Fillet085
  Base = -> Chamfer122 [Edge1,Edge7,Edge18,Edge4,Face12]
  BaseFeature = -> Chamfer122
  Radius = 0.4
FEATURE [Sketcher::SketchObject] Sketch669
  ExternalGeometry = -> [Fillet085]
  MapMode = 5
  Placement = pos=(0,0,43.1) rot=(0,0,1;0rad)
  Support = -> [Fillet085]
  sketch-geometry (1):
    g0: Circle CenterX=0 CenterY=10.15 CenterZ=0 NormalX=0 NormalY=0 NormalZ=1 AngleXU=0 Radius=3
  constraints (2):
    c: Coincident(g0,g-3)
    c: Radius(g0) = 3
FEATURE [PartDesign::Pocket] Pocket278
  BaseFeature = -> Fillet085
  Length = 5
  Length2 = 100
  Profile = -> Sketch669
  Type = 0
FEATURE [PartDesign::Body] Body154  label="MG996R004"
  Group = -> [Sketch685,Pad276,Sketch673,Pad274,Sketch671,Pad279,Sketch678,Pad272,Sketch680,Pad280,Sketch672,Pad271,Sketch684,Pad281,Sketch676,Pocket276,Sketch670,Pocket275,Sketch683,Pad268,Sketch674,Pocket274,Fillet086,Sketch677,Pad275,Sketch675,Pad267,Sketch681,Pad273,Chamfer122,Fillet085,Sketch669,Pocket278]
  Origin = -> Origin223
  Tip = -> Pocket278
FEATURE [App::Part] Part064  label="Servo004"
  Group = -> [Body154,Body158,Body157,Body155,Body156]
  Origin = -> Origin226
  Placement = pos=(-21.1341,-60.6,200.491) rot=(0.57735,0.57735,0.57735;2.0944rad)
FEATURE [Sketcher::SketchObject] Sketch689
  MapMode = 5
  Support = -> [XY_Plane227]
  sketch-geometry (8):
    g0: LineSegment StartX=0 StartY=3.17543 StartZ=0 EndX=-2.75 EndY=1.58771 EndZ=0
    g1: LineSegment StartX=-2.75 StartY=1.58771 StartZ=0 EndX=-2.75 EndY=-1.58771 EndZ=0
    g2: LineSegment StartX=-2.75 StartY=-1.58771 StartZ=0 EndX=0 EndY=-3.17543 EndZ=0
    g3: LineSegment StartX=0 StartY=-3.17543 StartZ=0 EndX=2.75 EndY=-1.58771 EndZ=0
    g4: LineSegment StartX=2.75 StartY=-1.58771 StartZ=0 EndX=2.75 EndY=1.58771 EndZ=0
    g5: LineSegment StartX=2.75 StartY=1.58771 StartZ=0 EndX=0 EndY=3.17543 EndZ=0
    g6: Circle [constr] CenterX=0 CenterY=0 CenterZ=0 NormalX=0 NormalY=0 NormalZ=1 AngleXU=0 Radius=3.17543
    g7: Circle CenterX=0 CenterY=0 CenterZ=0 NormalX=0 NormalY=0 NormalZ=1 AngleXU=0 Radius=1.5
  constraints (18):
    c: Coincident(g0,g1)
    c: Coincident(g1,g2)
    c: Coincident(g2,g3)
    c: Coincident(g3,g4)
    c: Coincident(g4,g5)
    c: Coincident(g5,g0)
    c: Equal(g0, g1-g5) x5
    c: PointOnObject(g0,g6)
    c: PointOnObject(g1,g6)
    c: PointOnObject(g2,g6)
    c: PointOnObject(g3,g6)
    c: PointOnObject(g4,g6)
    c: PointOnObject(g5,g6)
    c: Coincident(g6,g-1)
    c: PointOnObject(g5,g-2)
    c: DistanceX(g0,g4) = 5.5
    c: Coincident(g7,g-1)
    c: Radius(g7) = 1.5
FEATURE [PartDesign::Pad] Pad282  label="M3 Nut Primitive052"
  Length = 1.2
  Length2 = 1.2
  Profile = -> Sketch689
  Type = 4
FEATURE [Sketcher::SketchObject] Sketch690
  ExternalGeometry = -> [Pad282]
  MapMode = 5
  Placement = pos=(0,0,0) rot=(0.57735,0.57735,0.57735;2.0944rad)
  Support = -> [YZ_Plane227]
  sketch-geometry (6):
    g0: LineSegment StartX=-2.67543 StartY=1.2 StartZ=0 EndX=-3.67543 EndY=1.2 EndZ=0
    g1: LineSegment StartX=-3.67543 StartY=1.2 StartZ=0 EndX=-3.67543 EndY=-1.2 EndZ=0
    g2: LineSegment StartX=-3.67543 StartY=-1.2 StartZ=0 EndX=-2.67543 EndY=-1.2 EndZ=0
    g3: LineSegment StartX=-2.67543 StartY=-1.2 StartZ=0 EndX=-3.17543 EndY=-1 EndZ=0
    g4: LineSegment StartX=-3.17543 StartY=-1 StartZ=0 EndX=-3.17543 EndY=1 EndZ=0
    g5: LineSegment StartX=-3.17543 StartY=1 StartZ=0 EndX=-2.67543 EndY=1.2 EndZ=0
  constraints (15):
    c: Horizontal(g0)
    c: Coincident(g0,g1)
    c: Coincident(g1,g2)
    c: Coincident(g2,g3)
    c: Coincident(g3,g4)
    c: Coincident(g4,g5)
    c: Coincident(g5,g0)
    c: Symmetric(g4,g3,g-1)
    c: Symmetric(g0,g2,g-1)
    c: Symmetric(g1,g0,g-1)
    c: DistanceX(g0,g4) = 0.5
    c: DistanceY(g3,g4) = 2
    c: DistanceY(g1,g0) = 2.4
    c: PointOnObject(g3,g-3)
    c: DistanceX(g4,g0) = 0.5
FEATURE [PartDesign::Groove] Groove054  label="M3 Nut Smooth052"
  Angle = 360
  Axis = (-2e-16,3e-16,1)
  Base = (0,0,0)
  BaseFeature = -> Pad282
  Profile = -> Sketch690
  ReferenceAxis = -> Sketch690 [V_Axis]
  Reversed = true
FEATURE [PartDesign::Chamfer] Chamfer123  label="M3 Nut Smooth Hole052"
  Base = -> Groove054 [Edge24,Edge23]
  BaseFeature = -> Groove054
  Size = 0.2
FEATURE [PartDesign::Body] Body159  label="M3 Nut026"
  Group = -> [Sketch689,Pad282,Sketch690,Groove054,Chamfer123]
  Origin = -> Origin227
  Placement = pos=(3.9e-14,-65.6,176.35) rot=(0.57735,-0.57735,0.57735;4.18879rad)
  Tip = -> Chamfer123
FEATURE [Sketcher::SketchObject] Sketch691
  MapMode = 5
  Support = -> [XY_Plane228]
  sketch-geometry (8):
    g0: LineSegment StartX=0 StartY=3.17543 StartZ=0 EndX=-2.75 EndY=1.58771 EndZ=0
    g1: LineSegment StartX=-2.75 StartY=1.58771 StartZ=0 EndX=-2.75 EndY=-1.58771 EndZ=0
    g2: LineSegment StartX=-2.75 StartY=-1.58771 StartZ=0 EndX=0 EndY=-3.17543 EndZ=0
    g3: LineSegment StartX=0 StartY=-3.17543 StartZ=0 EndX=2.75 EndY=-1.58771 EndZ=0
    g4: LineSegment StartX=2.75 StartY=-1.58771 StartZ=0 EndX=2.75 EndY=1.58771 EndZ=0
    g5: LineSegment StartX=2.75 StartY=1.58771 StartZ=0 EndX=0 EndY=3.17543 EndZ=0
    g6: Circle [constr] CenterX=0 CenterY=0 CenterZ=0 NormalX=0 NormalY=0 NormalZ=1 AngleXU=0 Radius=3.17543
    g7: Circle CenterX=0 CenterY=0 CenterZ=0 NormalX=0 NormalY=0 NormalZ=1 AngleXU=0 Radius=1.5
  constraints (18):
    c: Coincident(g0,g1)
    c: Coincident(g1,g2)
    c: Coincident(g2,g3)
    c: Coincident(g3,g4)
    c: Coincident(g4,g5)
    c: Coincident(g5,g0)
    c: Equal(g0, g1-g5) x5
    c: PointOnObject(g0,g6)
    c: PointOnObject(g1,g6)
    c: PointOnObject(g2,g6)
    c: PointOnObject(g3,g6)
    c: PointOnObject(g4,g6)
    c: PointOnObject(g5,g6)
    c: Coincident(g6,g-1)
    c: PointOnObject(g5,g-2)
    c: DistanceX(g0,g4) = 5.5
    c: Coincident(g7,g-1)
    c: Radius(g7) = 1.5
FEATURE [PartDesign::Pad] Pad283  label="M3 Nut Primitive053"
  Length = 1.2
  Length2 = 1.2
  Profile = -> Sketch691
  Type = 4
FEATURE [Sketcher::SketchObject] Sketch692
  ExternalGeometry = -> [Pad283]
  MapMode = 5
  Placement = pos=(0,0,0) rot=(0.57735,0.57735,0.57735;2.0944rad)
  Support = -> [YZ_Plane228]
  sketch-geometry (6):
    g0: LineSegment StartX=-2.67543 StartY=1.2 StartZ=0 EndX=-3.67543 EndY=1.2 EndZ=0
    g1: LineSegment StartX=-3.67543 StartY=1.2 StartZ=0 EndX=-3.67543 EndY=-1.2 EndZ=0
    g2: LineSegment StartX=-3.67543 StartY=-1.2 StartZ=0 EndX=-2.67543 EndY=-1.2 EndZ=0
    g3: LineSegment StartX=-2.67543 StartY=-1.2 StartZ=0 EndX=-3.17543 EndY=-1 EndZ=0
    g4: LineSegment StartX=-3.17543 StartY=-1 StartZ=0 EndX=-3.17543 EndY=1 EndZ=0
    g5: LineSegment StartX=-3.17543 StartY=1 StartZ=0 EndX=-2.67543 EndY=1.2 EndZ=0
  constraints (15):
    c: Horizontal(g0)
    c: Coincident(g0,g1)
    c: Coincident(g1,g2)
    c: Coincident(g2,g3)
    c: Coincident(g3,g4)
    c: Coincident(g4,g5)
    c: Coincident(g5,g0)
    c: Symmetric(g4,g3,g-1)
    c: Symmetric(g0,g2,g-1)
    c: Symmetric(g1,g0,g-1)
    c: DistanceX(g0,g4) = 0.5
    c: DistanceY(g3,g4) = 2
    c: DistanceY(g1,g0) = 2.4
    c: PointOnObject(g3,g-3)
    c: DistanceX(g4,g0) = 0.5
FEATURE [PartDesign::Groove] Groove055  label="M3 Nut Smooth053"
  Angle = 360
  Axis = (-2e-16,3e-16,1)
  Base = (0,0,0)
  BaseFeature = -> Pad283
  Profile = -> Sketch692
  ReferenceAxis = -> Sketch692 [V_Axis]
  Reversed = true
FEATURE [PartDesign::Chamfer] Chamfer124  label="M3 Nut Smooth Hole053"
  Base = -> Groove055 [Edge24,Edge23]
  BaseFeature = -> Groove055
  Size = 0.2
FEATURE [PartDesign::Body] Body160  label="M3 Nut027"
  Group = -> [Sketch691,Pad283,Sketch692,Groove055,Chamfer124]
  Origin = -> Origin228
  Placement = pos=(1.5e-14,-55.6,176.35) rot=(0.57735,-0.57735,0.57735;4.18879rad)
  Tip = -> Chamfer124
FEATURE [Sketcher::SketchObject] Sketch693
  MapMode = 5
  Support = -> [XY_Plane229]
  sketch-geometry (8):
    g0: LineSegment StartX=0 StartY=3.17543 StartZ=0 EndX=-2.75 EndY=1.58771 EndZ=0
    g1: LineSegment StartX=-2.75 StartY=1.58771 StartZ=0 EndX=-2.75 EndY=-1.58771 EndZ=0
    g2: LineSegment StartX=-2.75 StartY=-1.58771 StartZ=0 EndX=0 EndY=-3.17543 EndZ=0
    g3: LineSegment StartX=0 StartY=-3.17543 StartZ=0 EndX=2.75 EndY=-1.58771 EndZ=0
    g4: LineSegment StartX=2.75 StartY=-1.58771 StartZ=0 EndX=2.75 EndY=1.58771 EndZ=0
    g5: LineSegment StartX=2.75 StartY=1.58771 StartZ=0 EndX=0 EndY=3.17543 EndZ=0
    g6: Circle [constr] CenterX=0 CenterY=0 CenterZ=0 NormalX=0 NormalY=0 NormalZ=1 AngleXU=0 Radius=3.17543
    g7: Circle CenterX=0 CenterY=0 CenterZ=0 NormalX=0 NormalY=0 NormalZ=1 AngleXU=0 Radius=1.5
  constraints (18):
    c: Coincident(g0,g1)
    c: Coincident(g1,g2)
    c: Coincident(g2,g3)
    c: Coincident(g3,g4)
    c: Coincident(g4,g5)
    c: Coincident(g5,g0)
    c: Equal(g0, g1-g5) x5
    c: PointOnObject(g0,g6)
    c: PointOnObject(g1,g6)
    c: PointOnObject(g2,g6)
    c: PointOnObject(g3,g6)
    c: PointOnObject(g4,g6)
    c: PointOnObject(g5,g6)
    c: Coincident(g6,g-1)
    c: PointOnObject(g5,g-2)
    c: DistanceX(g0,g4) = 5.5
    c: Coincident(g7,g-1)
    c: Radius(g7) = 1.5
FEATURE [PartDesign::Pad] Pad284  label="M3 Nut Primitive054"
  Length = 1.2
  Length2 = 1.2
  Profile = -> Sketch693
  Type = 4
FEATURE [Sketcher::SketchObject] Sketch694
  ExternalGeometry = -> [Pad284]
  MapMode = 5
  Placement = pos=(0,0,0) rot=(0.57735,0.57735,0.57735;2.0944rad)
  Support = -> [YZ_Plane229]
  sketch-geometry (6):
    g0: LineSegment StartX=-2.67543 StartY=1.2 StartZ=0 EndX=-3.67543 EndY=1.2 EndZ=0
    g1: LineSegment StartX=-3.67543 StartY=1.2 StartZ=0 EndX=-3.67543 EndY=-1.2 EndZ=0
    g2: LineSegment StartX=-3.67543 StartY=-1.2 StartZ=0 EndX=-2.67543 EndY=-1.2 EndZ=0
    g3: LineSegment StartX=-2.67543 StartY=-1.2 StartZ=0 EndX=-3.17543 EndY=-1 EndZ=0
    g4: LineSegment StartX=-3.17543 StartY=-1 StartZ=0 EndX=-3.17543 EndY=1 EndZ=0
    g5: LineSegment StartX=-3.17543 StartY=1 StartZ=0 EndX=-2.67543 EndY=1.2 EndZ=0
  constraints (15):
    c: Horizontal(g0)
    c: Coincident(g0,g1)
    c: Coincident(g1,g2)
    c: Coincident(g2,g3)
    c: Coincident(g3,g4)
    c: Coincident(g4,g5)
    c: Coincident(g5,g0)
    c: Symmetric(g4,g3,g-1)
    c: Symmetric(g0,g2,g-1)
    c: Symmetric(g1,g0,g-1)
    c: DistanceX(g0,g4) = 0.5
    c: DistanceY(g3,g4) = 2
    c: DistanceY(g1,g0) = 2.4
    c: PointOnObject(g3,g-3)
    c: DistanceX(g4,g0) = 0.5
FEATURE [PartDesign::Groove] Groove056  label="M3 Nut Smooth054"
  Angle = 360
  Axis = (-2e-16,3e-16,1)
  Base = (0,0,0)
  BaseFeature = -> Pad284
  Profile = -> Sketch694
  ReferenceAxis = -> Sketch694 [V_Axis]
  Reversed = true
FEATURE [PartDesign::Chamfer] Chamfer125  label="M3 Nut Smooth Hole054"
  Base = -> Groove056 [Edge24,Edge23]
  BaseFeature = -> Groove056
  Size = 0.2
FEATURE [PartDesign::Body] Body161  label="M3 Nut028"
  Group = -> [Sketch693,Pad284,Sketch694,Groove056,Chamfer125]
  Origin = -> Origin229
  Placement = pos=(5e-14,-65.6,224.85) rot=(0.57735,-0.57735,0.57735;4.18879rad)
  Tip = -> Chamfer125
FEATURE [Sketcher::SketchObject] Sketch695
  MapMode = 5
  Support = -> [XY_Plane230]
  sketch-geometry (8):
    g0: LineSegment StartX=0 StartY=3.17543 StartZ=0 EndX=-2.75 EndY=1.58771 EndZ=0
    g1: LineSegment StartX=-2.75 StartY=1.58771 StartZ=0 EndX=-2.75 EndY=-1.58771 EndZ=0
    g2: LineSegment StartX=-2.75 StartY=-1.58771 StartZ=0 EndX=0 EndY=-3.17543 EndZ=0
    g3: LineSegment StartX=0 StartY=-3.17543 StartZ=0 EndX=2.75 EndY=-1.58771 EndZ=0
    g4: LineSegment StartX=2.75 StartY=-1.58771 StartZ=0 EndX=2.75 EndY=1.58771 EndZ=0
    g5: LineSegment StartX=2.75 StartY=1.58771 StartZ=0 EndX=0 EndY=3.17543 EndZ=0
    g6: Circle [constr] CenterX=0 CenterY=0 CenterZ=0 NormalX=0 NormalY=0 NormalZ=1 AngleXU=0 Radius=3.17543
    g7: Circle CenterX=0 CenterY=0 CenterZ=0 NormalX=0 NormalY=0 NormalZ=1 AngleXU=0 Radius=1.5
  constraints (18):
    c: Coincident(g0,g1)
    c: Coincident(g1,g2)
    c: Coincident(g2,g3)
    c: Coincident(g3,g4)
    c: Coincident(g4,g5)
    c: Coincident(g5,g0)
    c: Equal(g0, g1-g5) x5
    c: PointOnObject(g0,g6)
    c: PointOnObject(g1,g6)
    c: PointOnObject(g2,g6)
    c: PointOnObject(g3,g6)
    c: PointOnObject(g4,g6)
    c: PointOnObject(g5,g6)
    c: Coincident(g6,g-1)
    c: PointOnObject(g5,g-2)
    c: DistanceX(g0,g4) = 5.5
    c: Coincident(g7,g-1)
    c: Radius(g7) = 1.5
FEATURE [PartDesign::Pad] Pad285  label="M3 Nut Primitive055"
  Length = 1.2
  Length2 = 1.2
  Profile = -> Sketch695
  Type = 4
FEATURE [Sketcher::SketchObject] Sketch696
  ExternalGeometry = -> [Pad285]
  MapMode = 5
  Placement = pos=(0,0,0) rot=(0.57735,0.57735,0.57735;2.0944rad)
  Support = -> [YZ_Plane230]
  sketch-geometry (6):
    g0: LineSegment StartX=-2.67543 StartY=1.2 StartZ=0 EndX=-3.67543 EndY=1.2 EndZ=0
    g1: LineSegment StartX=-3.67543 StartY=1.2 StartZ=0 EndX=-3.67543 EndY=-1.2 EndZ=0
    g2: LineSegment StartX=-3.67543 StartY=-1.2 StartZ=0 EndX=-2.67543 EndY=-1.2 EndZ=0
    g3: LineSegment StartX=-2.67543 StartY=-1.2 StartZ=0 EndX=-3.17543 EndY=-1 EndZ=0
    g4: LineSegment StartX=-3.17543 StartY=-1 StartZ=0 EndX=-3.17543 EndY=1 EndZ=0
    g5: LineSegment StartX=-3.17543 StartY=1 StartZ=0 EndX=-2.67543 EndY=1.2 EndZ=0
  constraints (15):
    c: Horizontal(g0)
    c: Coincident(g0,g1)
    c: Coincident(g1,g2)
    c: Coincident(g2,g3)
    c: Coincident(g3,g4)
    c: Coincident(g4,g5)
    c: Coincident(g5,g0)
    c: Symmetric(g4,g3,g-1)
    c: Symmetric(g0,g2,g-1)
    c: Symmetric(g1,g0,g-1)
    c: DistanceX(g0,g4) = 0.5
    c: DistanceY(g3,g4) = 2
    c: DistanceY(g1,g0) = 2.4
    c: PointOnObject(g3,g-3)
    c: DistanceX(g4,g0) = 0.5
FEATURE [PartDesign::Groove] Groove057  label="M3 Nut Smooth055"
  Angle = 360
  Axis = (-2e-16,3e-16,1)
  Base = (0,0,0)
  BaseFeature = -> Pad285
  Profile = -> Sketch696
  ReferenceAxis = -> Sketch696 [V_Axis]
  Reversed = true
FEATURE [PartDesign::Chamfer] Chamfer126  label="M3 Nut Smooth Hole055"
  Base = -> Groove057 [Edge24,Edge23]
  BaseFeature = -> Groove057
  Size = 0.2
FEATURE [PartDesign::Body] Body162  label="M3 Nut029"
  Group = -> [Sketch695,Pad285,Sketch696,Groove057,Chamfer126]
  Origin = -> Origin230
  Placement = pos=(5e-14,-55.6,224.85) rot=(0.57735,-0.57735,0.57735;4.18879rad)
  Tip = -> Chamfer126
FEATURE [Sketcher::SketchObject] Sketch698
  MapMode = 5
  Support = -> [XY_Plane232]
  sketch-geometry (1):
    g0: Circle CenterX=0 CenterY=0 CenterZ=0 NormalX=0 NormalY=0 NormalZ=1 AngleXU=0 Radius=2.75
  constraints (2):
    c: Coincident(g0,g-1)
    c: Radius(g0) = 2.75
FEATURE [PartDesign::Pad] Pad287  label="M3x20 Head020"
  Length = 3
  Length2 = 100
  Profile = -> Sketch698
  Type = 0
FEATURE [Sketcher::SketchObject] Sketch699
  MapMode = 5
  Placement = pos=(0,0,3) rot=(0,0,1;0rad)
  Support = -> [Pad287]
  sketch-geometry (1):
    g0: Circle CenterX=0 CenterY=0 CenterZ=0 NormalX=0 NormalY=0 NormalZ=1 AngleXU=0 Radius=1.5
  constraints (2):
    c: Coincident(g0,g-1)
    c: Radius(g0) = 1.5
FEATURE [PartDesign::Pad] Pad286  label="M3x20 Thread020"
  BaseFeature = -> Pad287
  Length = 20
  Length2 = 100
  Profile = -> Sketch699
  Type = 0
FEATURE [Sketcher::SketchObject] Sketch697
  MapMode = 5
  Placement = pos=(0,0,0) rot=(1,0,0;3.14159rad)
  Support = -> [Pad286]
  sketch-geometry (7):
    g0: LineSegment StartX=1.275 StartY=0.736122 StartZ=0 EndX=0 EndY=1.47224 EndZ=0
    g1: LineSegment StartX=0 StartY=1.47224 StartZ=0 EndX=-1.275 EndY=0.736122 EndZ=0
    g2: LineSegment StartX=-1.275 StartY=0.736122 StartZ=0 EndX=-1.275 EndY=-0.736122 EndZ=0
    g3: LineSegment StartX=-1.275 StartY=-0.736122 StartZ=0 EndX=1.34766e-11 EndY=-1.47224 EndZ=0
    g4: LineSegment StartX=1.34766e-11 StartY=-1.47224 StartZ=0 EndX=1.275 EndY=-0.736122 EndZ=0
    g5: LineSegment StartX=1.275 StartY=-0.736122 StartZ=0 EndX=1.275 EndY=0.736122 EndZ=0
    g6: Circle [constr] CenterX=0 CenterY=0 CenterZ=0 NormalX=0 NormalY=0 NormalZ=1 AngleXU=0 Radius=1.47224
  constraints (16):
    c: Coincident(g0,g1)
    c: Coincident(g1,g2)
    c: Coincident(g2,g3)
    c: Coincident(g3,g4)
    c: Coincident(g4,g5)
    c: Coincident(g5,g0)
    c: Equal(g0, g1-g5) x5
    c: PointOnObject(g0,g6)
    c: PointOnObject(g1,g6)
    c: PointOnObject(g2,g6)
    c: PointOnObject(g3,g6)
    c: PointOnObject(g4,g6)
    c: PointOnObject(g5,g6)
    c: Coincident(g6,g-1)
    c: PointOnObject(g0,g-2)
    c: DistanceX(g1,g0) = 2.55
FEATURE [PartDesign::Pocket] Pocket279  label="M3x20 Wrench020"
  BaseFeature = -> Pad286
  Length = 1.3
  Length2 = 100
  Profile = -> Sketch697
  Type = 0
FEATURE [PartDesign::Chamfer] Chamfer127  label="M3x20 Smooth020"
  Base = -> Pocket279 [Face11,Edge2,Edge24,Edge3]
  BaseFeature = -> Pocket279
  Size = 0.2
FEATURE [PartDesign::Body] Body163  label="M3x036"
  Group = -> [Sketch698,Pad287,Sketch699,Pad286,Sketch697,Pocket279,Chamfer127]
  Origin = -> Origin232
  Placement = pos=(11.25,-65.6,224.85) rot=(0,-1,0;1.5708rad)
  Tip = -> Chamfer127
FEATURE [Sketcher::SketchObject] Sketch701
  MapMode = 5
  Support = -> [XY_Plane233]
  sketch-geometry (1):
    g0: Circle CenterX=0 CenterY=0 CenterZ=0 NormalX=0 NormalY=0 NormalZ=1 AngleXU=0 Radius=2.75
  constraints (2):
    c: Coincident(g0,g-1)
    c: Radius(g0) = 2.75
FEATURE [PartDesign::Pad] Pad289  label="M3x20 Head021"
  Length = 3
  Length2 = 100
  Profile = -> Sketch701
  Type = 0
FEATURE [Sketcher::SketchObject] Sketch702
  MapMode = 5
  Placement = pos=(0,0,3) rot=(0,0,1;0rad)
  Support = -> [Pad289]
  sketch-geometry (1):
    g0: Circle CenterX=0 CenterY=0 CenterZ=0 NormalX=0 NormalY=0 NormalZ=1 AngleXU=0 Radius=1.5
  constraints (2):
    c: Coincident(g0,g-1)
    c: Radius(g0) = 1.5
FEATURE [PartDesign::Pad] Pad288  label="M3x20 Thread021"
  BaseFeature = -> Pad289
  Length = 20
  Length2 = 100
  Profile = -> Sketch702
  Type = 0
FEATURE [Sketcher::SketchObject] Sketch700
  MapMode = 5
  Placement = pos=(0,0,0) rot=(1,0,0;3.14159rad)
  Support = -> [Pad288]
  sketch-geometry (7):
    g0: LineSegment StartX=1.275 StartY=0.736122 StartZ=0 EndX=0 EndY=1.47224 EndZ=0
    g1: LineSegment StartX=0 StartY=1.47224 StartZ=0 EndX=-1.275 EndY=0.736122 EndZ=0
    g2: LineSegment StartX=-1.275 StartY=0.736122 StartZ=0 EndX=-1.275 EndY=-0.736122 EndZ=0
    g3: LineSegment StartX=-1.275 StartY=-0.736122 StartZ=0 EndX=1.34766e-11 EndY=-1.47224 EndZ=0
    g4: LineSegment StartX=1.34766e-11 StartY=-1.47224 StartZ=0 EndX=1.275 EndY=-0.736122 EndZ=0
    g5: LineSegment StartX=1.275 StartY=-0.736122 StartZ=0 EndX=1.275 EndY=0.736122 EndZ=0
    g6: Circle [constr] CenterX=0 CenterY=0 CenterZ=0 NormalX=0 NormalY=0 NormalZ=1 AngleXU=0 Radius=1.47224
  constraints (16):
    c: Coincident(g0,g1)
    c: Coincident(g1,g2)
    c: Coincident(g2,g3)
    c: Coincident(g3,g4)
    c: Coincident(g4,g5)
    c: Coincident(g5,g0)
    c: Equal(g0, g1-g5) x5
    c: PointOnObject(g0,g6)
    c: PointOnObject(g1,g6)
    c: PointOnObject(g2,g6)
    c: PointOnObject(g3,g6)
    c: PointOnObject(g4,g6)
    c: PointOnObject(g5,g6)
    c: Coincident(g6,g-1)
    c: PointOnObject(g0,g-2)
    c: DistanceX(g1,g0) = 2.55
FEATURE [PartDesign::Pocket] Pocket280  label="M3x20 Wrench021"
  BaseFeature = -> Pad288
  Length = 1.3
  Length2 = 100
  Profile = -> Sketch700
  Type = 0
FEATURE [PartDesign::Chamfer] Chamfer128  label="M3x20 Smooth021"
  Base = -> Pocket280 [Face11,Edge2,Edge24,Edge3]
  BaseFeature = -> Pocket280
  Size = 0.2
FEATURE [PartDesign::Body] Body164  label="M3x037"
  Group = -> [Sketch701,Pad289,Sketch702,Pad288,Sketch700,Pocket280,Chamfer128]
  Origin = -> Origin233
  Placement = pos=(11.25,-55.6,224.85) rot=(0,-1,0;1.5708rad)
  Tip = -> Chamfer128
FEATURE [Sketcher::SketchObject] Sketch704
  MapMode = 5
  Support = -> [XY_Plane234]
  sketch-geometry (1):
    g0: Circle CenterX=0 CenterY=0 CenterZ=0 NormalX=0 NormalY=0 NormalZ=1 AngleXU=0 Radius=2.75
  constraints (2):
    c: Coincident(g0,g-1)
    c: Radius(g0) = 2.75
FEATURE [PartDesign::Pad] Pad291  label="M3x20 Head022"
  Length = 3
  Length2 = 100
  Profile = -> Sketch704
  Type = 0
FEATURE [Sketcher::SketchObject] Sketch705
  MapMode = 5
  Placement = pos=(0,0,3) rot=(0,0,1;0rad)
  Support = -> [Pad291]
  sketch-geometry (1):
    g0: Circle CenterX=0 CenterY=0 CenterZ=0 NormalX=0 NormalY=0 NormalZ=1 AngleXU=0 Radius=1.5
  constraints (2):
    c: Coincident(g0,g-1)
    c: Radius(g0) = 1.5
FEATURE [PartDesign::Pad] Pad290  label="M3x20 Thread022"
  BaseFeature = -> Pad291
  Length = 20
  Length2 = 100
  Profile = -> Sketch705
  Type = 0
FEATURE [Sketcher::SketchObject] Sketch703
  MapMode = 5
  Placement = pos=(0,0,0) rot=(1,0,0;3.14159rad)
  Support = -> [Pad290]
  sketch-geometry (7):
    g0: LineSegment StartX=1.275 StartY=0.736122 StartZ=0 EndX=0 EndY=1.47224 EndZ=0
    g1: LineSegment StartX=0 StartY=1.47224 StartZ=0 EndX=-1.275 EndY=0.736122 EndZ=0
    g2: LineSegment StartX=-1.275 StartY=0.736122 StartZ=0 EndX=-1.275 EndY=-0.736122 EndZ=0
    g3: LineSegment StartX=-1.275 StartY=-0.736122 StartZ=0 EndX=1.34766e-11 EndY=-1.47224 EndZ=0
    g4: LineSegment StartX=1.34766e-11 StartY=-1.47224 StartZ=0 EndX=1.275 EndY=-0.736122 EndZ=0
    g5: LineSegment StartX=1.275 StartY=-0.736122 StartZ=0 EndX=1.275 EndY=0.736122 EndZ=0
    g6: Circle [constr] CenterX=0 CenterY=0 CenterZ=0 NormalX=0 NormalY=0 NormalZ=1 AngleXU=0 Radius=1.47224
  constraints (16):
    c: Coincident(g0,g1)
    c: Coincident(g1,g2)
    c: Coincident(g2,g3)
    c: Coincident(g3,g4)
    c: Coincident(g4,g5)
    c: Coincident(g5,g0)
    c: Equal(g0, g1-g5) x5
    c: PointOnObject(g0,g6)
    c: PointOnObject(g1,g6)
    c: PointOnObject(g2,g6)
    c: PointOnObject(g3,g6)
    c: PointOnObject(g4,g6)
    c: PointOnObject(g5,g6)
    c: Coincident(g6,g-1)
    c: PointOnObject(g0,g-2)
    c: DistanceX(g1,g0) = 2.55
FEATURE [PartDesign::Pocket] Pocket281  label="M3x20 Wrench022"
  BaseFeature = -> Pad290
  Length = 1.3
  Length2 = 100
  Profile = -> Sketch703
  Type = 0
FEATURE [PartDesign::Chamfer] Chamfer129  label="M3x20 Smooth022"
  Base = -> Pocket281 [Face11,Edge2,Edge24,Edge3]
  BaseFeature = -> Pocket281
  Size = 0.2
FEATURE [PartDesign::Body] Body165  label="M3x038"
  Group = -> [Sketch704,Pad291,Sketch705,Pad290,Sketch703,Pocket281,Chamfer129]
  Origin = -> Origin234
  Placement = pos=(11.3,-65.6,176.35) rot=(0,-1,0;1.5708rad)
  Tip = -> Chamfer129
FEATURE [Sketcher::SketchObject] Sketch707
  MapMode = 5
  Support = -> [XY_Plane235]
  sketch-geometry (1):
    g0: Circle CenterX=0 CenterY=0 CenterZ=0 NormalX=0 NormalY=0 NormalZ=1 AngleXU=0 Radius=2.75
  constraints (2):
    c: Coincident(g0,g-1)
    c: Radius(g0) = 2.75
FEATURE [PartDesign::Pad] Pad293  label="M3x20 Head023"
  Length = 3
  Length2 = 100
  Profile = -> Sketch707
  Type = 0
FEATURE [Sketcher::SketchObject] Sketch708
  MapMode = 5
  Placement = pos=(0,0,3) rot=(0,0,1;0rad)
  Support = -> [Pad293]
  sketch-geometry (1):
    g0: Circle CenterX=0 CenterY=0 CenterZ=0 NormalX=0 NormalY=0 NormalZ=1 AngleXU=0 Radius=1.5
  constraints (2):
    c: Coincident(g0,g-1)
    c: Radius(g0) = 1.5
FEATURE [PartDesign::Pad] Pad292  label="M3x20 Thread023"
  BaseFeature = -> Pad293
  Length = 20
  Length2 = 100
  Profile = -> Sketch708
  Type = 0
FEATURE [Sketcher::SketchObject] Sketch706
  MapMode = 5
  Placement = pos=(0,0,0) rot=(1,0,0;3.14159rad)
  Support = -> [Pad292]
  sketch-geometry (7):
    g0: LineSegment StartX=1.275 StartY=0.736122 StartZ=0 EndX=0 EndY=1.47224 EndZ=0
    g1: LineSegment StartX=0 StartY=1.47224 StartZ=0 EndX=-1.275 EndY=0.736122 EndZ=0
    g2: LineSegment StartX=-1.275 StartY=0.736122 StartZ=0 EndX=-1.275 EndY=-0.736122 EndZ=0
    g3: LineSegment StartX=-1.275 StartY=-0.736122 StartZ=0 EndX=1.34766e-11 EndY=-1.47224 EndZ=0
    g4: LineSegment StartX=1.34766e-11 StartY=-1.47224 StartZ=0 EndX=1.275 EndY=-0.736122 EndZ=0
    g5: LineSegment StartX=1.275 StartY=-0.736122 StartZ=0 EndX=1.275 EndY=0.736122 EndZ=0
    g6: Circle [constr] CenterX=0 CenterY=0 CenterZ=0 NormalX=0 NormalY=0 NormalZ=1 AngleXU=0 Radius=1.47224
  constraints (16):
    c: Coincident(g0,g1)
    c: Coincident(g1,g2)
    c: Coincident(g2,g3)
    c: Coincident(g3,g4)
    c: Coincident(g4,g5)
    c: Coincident(g5,g0)
    c: Equal(g0, g1-g5) x5
    c: PointOnObject(g0,g6)
    c: PointOnObject(g1,g6)
    c: PointOnObject(g2,g6)
    c: PointOnObject(g3,g6)
    c: PointOnObject(g4,g6)
    c: PointOnObject(g5,g6)
    c: Coincident(g6,g-1)
    c: PointOnObject(g0,g-2)
    c: DistanceX(g1,g0) = 2.55
FEATURE [PartDesign::Pocket] Pocket282  label="M3x20 Wrench023"
  BaseFeature = -> Pad292
  Length = 1.3
  Length2 = 100
  Profile = -> Sketch706
  Type = 0
FEATURE [PartDesign::Chamfer] Chamfer130  label="M3x20 Smooth023"
  Base = -> Pocket282 [Face11,Edge2,Edge24,Edge3]
  BaseFeature = -> Pocket282
  Size = 0.2
FEATURE [PartDesign::Body] Body166  label="M3x039"
  Group = -> [Sketch707,Pad293,Sketch708,Pad292,Sketch706,Pocket282,Chamfer130]
  Origin = -> Origin235
  Placement = pos=(11.3,-55.6,176.35) rot=(0,-1,0;1.5708rad)
  Tip = -> Chamfer130
FEATURE [App::Part] Part066  label="Servo Scres"
  Group = -> [Body163,Body164,Body165,Body166]
  Origin = -> Origin236
FEATURE [Sketcher::SketchObject] Sketch711
  MapMode = 5
  Placement = pos=(0,0,0) rot=(1,0,0;1.5708rad)
  Support = -> [XZ_Plane387]
  sketch-geometry (8):
    g0: LineSegment StartX=-1.5 StartY=2.25 StartZ=0 EndX=-3.25 EndY=2.25 EndZ=0
    g1: LineSegment StartX=-3.25 StartY=2.25 StartZ=0 EndX=-3.25 EndY=1.25 EndZ=0
    g2: LineSegment StartX=-3.25 StartY=1.25 StartZ=0 EndX=-2 EndY=1.25 EndZ=0
    g3: LineSegment StartX=-2 StartY=1.25 StartZ=0 EndX=-2 EndY=-1.25 EndZ=0
    g4: LineSegment StartX=-2 StartY=-1.25 StartZ=0 EndX=-3.25 EndY=-1.25 EndZ=0
    g5: LineSegment StartX=-3.25 StartY=-1.25 StartZ=0 EndX=-3.25 EndY=-2.25 EndZ=0
    g6: LineSegment StartX=-3.25 StartY=-2.25 StartZ=0 EndX=-1.5 EndY=-2.25 EndZ=0
    g7: LineSegment StartX=-1.5 StartY=-2.25 StartZ=0 EndX=-1.5 EndY=2.25 EndZ=0
  constraints (23):
    c: Horizontal(g0)
    c: Coincident(g0,g1)
    c: Vertical(g1)
    c: Coincident(g1,g2)
    c: Horizontal(g2)
    c: Coincident(g2,g3)
    c: Vertical(g3)
    c: Coincident(g3,g4)
    c: Horizontal(g4)
    c: Coincident(g4,g5)
    c: Vertical(g5)
    c: Coincident(g5,g6)
    c: Horizontal(g6)
    c: Coincident(g6,g7)
    c: Vertical(g7)
    c: Coincident(g0,g7)
    c: Equal(g1,g5)
    c: Symmetric(g4,g1,g-1)
    c: DistanceX(g0,g-1) = 1.5
    c: DistanceY(g3,g3) = 2.5
    c: DistanceY(g7,g7) = 4.5
    c: DistanceX(g0,g-1) = 3.25
    c: DistanceX(g2,g-1) = 2
FEATURE [Sketcher::SketchObject] Sketch716
  MapMode = 5
  Support = -> [XY_Plane256]
FEATURE [Sketcher::SketchObject] Sketch719
  MapMode = 5
  Support = -> [XY_Plane240]
  sketch-geometry (64):
    g0: LineSegment [constr] StartX=-3.75 StartY=6.49519 StartZ=0 EndX=-7.5 EndY=0 EndZ=0
    g1: LineSegment [constr] StartX=-7.5 StartY=0 StartZ=0 EndX=-3.75 EndY=-6.49519 EndZ=0
    g2: LineSegment [constr] StartX=-3.75 StartY=-6.49519 StartZ=0 EndX=3.75 EndY=-6.49519 EndZ=0
    g3: LineSegment [constr] StartX=3.75 StartY=-6.49519 StartZ=0 EndX=7.5 EndY=0 EndZ=0
    g4: LineSegment [constr] StartX=7.5 StartY=0 StartZ=0 EndX=3.75 EndY=6.49519 EndZ=0
    g5: LineSegment [constr] StartX=3.75 StartY=6.49519 StartZ=0 EndX=-3.75 EndY=6.49519 EndZ=0
    g6: Circle [constr] CenterX=0 CenterY=0 CenterZ=0 NormalX=0 NormalY=0 NormalZ=1 AngleXU=0 Radius=7.5
    g7: LineSegment [constr] StartX=0 StartY=7.5 StartZ=0 EndX=-6.49519 EndY=3.75 EndZ=0
    g8: LineSegment [constr] StartX=-6.49519 StartY=3.75 StartZ=0 EndX=-6.49519 EndY=-3.75 EndZ=0
    g9: LineSegment [constr] StartX=-6.49519 StartY=-3.75 StartZ=0 EndX=9.8e-15 EndY=-7.5 EndZ=0
    g10: LineSegment [constr] StartX=9.8e-15 StartY=-7.5 StartZ=0 EndX=6.49519 EndY=-3.75 EndZ=0
    g11: LineSegment [constr] StartX=6.49519 StartY=-3.75 StartZ=0 EndX=6.49519 EndY=3.75 EndZ=0
    g12: LineSegment [constr] StartX=6.49519 StartY=3.75 StartZ=0 EndX=0 EndY=7.5 EndZ=0
    g13: Circle [constr] CenterX=0 CenterY=0 CenterZ=0 NormalX=0 NormalY=0 NormalZ=1 AngleXU=0 Radius=7.5
    g14: LineSegment [constr] StartX=0 StartY=10.5 StartZ=0 EndX=-9.09327 EndY=5.25 EndZ=0
    g15: LineSegment [constr] StartX=-9.09327 StartY=5.25 StartZ=0 EndX=-9.09327 EndY=-5.25 EndZ=0
    g16: LineSegment [constr] StartX=-9.09327 StartY=-5.25 StartZ=0 EndX=-1.42e-14 EndY=-10.5 EndZ=0
    g17: LineSegment [constr] StartX=-1.42e-14 StartY=-10.5 StartZ=0 EndX=9.09327 EndY=-5.25 EndZ=0
    g18: LineSegment [constr] StartX=9.09327 StartY=-5.25 StartZ=0 EndX=9.09327 EndY=5.25 EndZ=0
    g19: LineSegment [constr] StartX=9.09327 StartY=5.25 StartZ=0 EndX=0 EndY=10.5 EndZ=0
    g20: Circle [constr] CenterX=0 CenterY=0 CenterZ=0 NormalX=0 NormalY=0 NormalZ=1 AngleXU=0 Radius=10.5
    g21: LineSegment [constr] StartX=0 StartY=13.5 StartZ=0 EndX=-11.6913 EndY=6.75 EndZ=0
    g22: LineSegment [constr] StartX=-11.6913 StartY=6.75 StartZ=0 EndX=-11.6913 EndY=-6.75 EndZ=0
    g23: LineSegment [constr] StartX=-11.6913 StartY=-6.75 StartZ=0 EndX=0 EndY=-13.5 EndZ=0
    g24: LineSegment [constr] StartX=0 StartY=-13.5 StartZ=0 EndX=11.6913 EndY=-6.75 EndZ=0
    g25: LineSegment [constr] StartX=11.6913 StartY=-6.75 StartZ=0 EndX=11.6913 EndY=6.75 EndZ=0
    g26: LineSegment [constr] StartX=11.6913 StartY=6.75 StartZ=0 EndX=0 EndY=13.5 EndZ=0
    g27: Circle [constr] CenterX=0 CenterY=0 CenterZ=0 NormalX=0 NormalY=0 NormalZ=1 AngleXU=0 Radius=13.5
    g28: ArcOfCircle CenterX=0 CenterY=13.5 CenterZ=0 NormalX=0 NormalY=0 NormalZ=1 AngleXU=0 Radius=2.5 StartAngle=0.171439 EndAngle=2.97015
    g29: ArcOfCircle CenterX=11.6913 CenterY=6.75 CenterZ=0 NormalX=0 NormalY=0 NormalZ=1 AngleXU=0 Radius=2.5 StartAngle=5.40743 EndAngle=8.20614
    g30: ArcOfCircle CenterX=11.6913 CenterY=-6.75 CenterZ=0 NormalX=0 NormalY=0 NormalZ=1 AngleXU=0 Radius=2.5 StartAngle=4.36023 EndAngle=7.15894
    g31: ArcOfCircle CenterX=0 CenterY=-13.5 CenterZ=0 NormalX=0 NormalY=0 NormalZ=1 AngleXU=0 Radius=2.5 StartAngle=3.31303 EndAngle=6.11175
    g32: ArcOfCircle CenterX=-11.6913 CenterY=-6.75 CenterZ=0 NormalX=0 NormalY=0 NormalZ=1 AngleXU=0 Radius=2.5 StartAngle=2.26583 EndAngle=5.06455
    g33: ArcOfCircle CenterX=-11.6913 CenterY=6.75 CenterZ=0 NormalX=0 NormalY=0 NormalZ=1 AngleXU=0 Radius=2.5 StartAngle=1.21864 EndAngle=4.01735
    g34: LineSegment StartX=-10.829 StartY=9.09658 StartZ=0 EndX=-3.75 EndY=6.49519 EndZ=0
    g35: LineSegment StartX=-3.75 StartY=6.49519 StartZ=0 EndX=-2.46335 EndY=13.9265 EndZ=0
    g36: LineSegment StartX=2.46335 StartY=13.9265 StartZ=0 EndX=3.75 EndY=6.49519 EndZ=0
    g37: LineSegment StartX=3.75 StartY=6.49519 StartZ=0 EndX=10.829 EndY=9.09658 EndZ=0
    g38: LineSegment StartX=13.2924 StartY=4.82993 StartZ=0 EndX=7.5 EndY=0 EndZ=0
    g39: LineSegment StartX=7.5 StartY=0 StartZ=0 EndX=13.2924 EndY=-4.82993 EndZ=0
    g40: LineSegment StartX=10.829 StartY=-9.09658 StartZ=0 EndX=3.75 EndY=-6.49519 EndZ=0
    g41: LineSegment StartX=3.75 StartY=-6.49519 StartZ=0 EndX=2.46335 EndY=-13.9265 EndZ=0
    g42: LineSegment StartX=-2.46335 StartY=-13.9265 StartZ=0 EndX=-3.75 EndY=-6.49519 EndZ=0
    g43: LineSegment StartX=-3.75 StartY=-6.49519 StartZ=0 EndX=-10.829 EndY=-9.09658 EndZ=0
    g44: LineSegment StartX=-13.2924 StartY=-4.82993 StartZ=0 EndX=-7.5 EndY=0 EndZ=0
    g45: LineSegment StartX=-7.5 StartY=0 StartZ=0 EndX=-13.2924 EndY=4.82993 EndZ=0
    g46: Circle CenterX=-11.6913 CenterY=6.75 CenterZ=0 NormalX=0 NormalY=0 NormalZ=1 AngleXU=0 Radius=0.75
    g47: Circle CenterX=-9.09327 CenterY=5.25 CenterZ=0 NormalX=0 NormalY=0 NormalZ=1 AngleXU=0 Radius=0.75
    g48: Circle CenterX=-6.49519 CenterY=3.75 CenterZ=0 NormalX=0 NormalY=0 NormalZ=1 AngleXU=0 Radius=0.75
    g49: Circle CenterX=0 CenterY=13.5 CenterZ=0 NormalX=0 NormalY=0 NormalZ=1 AngleXU=0 Radius=0.75
    g50: Circle CenterX=0 CenterY=10.5 CenterZ=0 NormalX=0 NormalY=0 NormalZ=1 AngleXU=0 Radius=0.75
    g51: Circle CenterX=0 CenterY=7.5 CenterZ=0 NormalX=0 NormalY=0 NormalZ=1 AngleXU=0 Radius=0.75
    g52: Circle CenterX=11.6913 CenterY=6.75 CenterZ=0 NormalX=0 NormalY=0 NormalZ=1 AngleXU=0 Radius=0.75
    g53: Circle CenterX=9.09327 CenterY=5.25 CenterZ=0 NormalX=0 NormalY=0 NormalZ=1 AngleXU=0 Radius=0.75
    g54: Circle CenterX=6.49519 CenterY=3.75 CenterZ=0 NormalX=0 NormalY=0 NormalZ=1 AngleXU=0 Radius=0.75
    g55: Circle CenterX=11.6913 CenterY=-6.75 CenterZ=0 NormalX=0 NormalY=0 NormalZ=1 AngleXU=0 Radius=0.75
    g56: Circle CenterX=9.09327 CenterY=-5.25 CenterZ=0 NormalX=0 NormalY=0 NormalZ=1 AngleXU=0 Radius=0.75
    g57: Circle CenterX=6.49519 CenterY=-3.75 CenterZ=0 NormalX=0 NormalY=0 NormalZ=1 AngleXU=0 Radius=0.75
    g58: Circle CenterX=9.8e-15 CenterY=-7.5 CenterZ=0 NormalX=0 NormalY=0 NormalZ=1 AngleXU=0 Radius=0.75
    g59: Circle CenterX=-1.42e-14 CenterY=-10.5 CenterZ=0 NormalX=0 NormalY=0 NormalZ=1 AngleXU=0 Radius=0.75
    g60: Circle CenterX=0 CenterY=-13.5 CenterZ=0 NormalX=0 NormalY=0 NormalZ=1 AngleXU=0 Radius=0.75
    g61: Circle CenterX=-11.6913 CenterY=-6.75 CenterZ=0 NormalX=0 NormalY=0 NormalZ=1 AngleXU=0 Radius=0.75
    g62: Circle CenterX=-9.09327 CenterY=-5.25 CenterZ=0 NormalX=0 NormalY=0 NormalZ=1 AngleXU=0 Radius=0.75
    g63: Circle CenterX=-6.49519 CenterY=-3.75 CenterZ=0 NormalX=0 NormalY=0 NormalZ=1 AngleXU=0 Radius=0.75
  constraints (136):
    c: Coincident(g0,g1)
    c: Coincident(g1,g2)
    c: Coincident(g2,g3)
    c: Coincident(g3,g4)
    c: Coincident(g4,g5)
    c: Coincident(g5,g0)
    c: Equal(g0, g1-g5) x5
    c: PointOnObject(g0,g6)
    c: PointOnObject(g1,g6)
    c: PointOnObject(g2,g6)
    c: PointOnObject(g3,g6)
    c: PointOnObject(g4,g6)
    c: PointOnObject(g5,g6)
    c: Coincident(g6,g-1)
    c: Coincident(g7,g8)
    c: Coincident(g8,g9)
    c: Coincident(g9,g10)
    c: Coincident(g10,g11)
    c: Coincident(g11,g12)
    c: Coincident(g12,g7)
    c: Equal(g7, g8-g12) x5
    c: PointOnObject(g7,g13)
    c: PointOnObject(g8,g13)
    c: PointOnObject(g9,g13)
    c: PointOnObject(g10,g13)
    c: PointOnObject(g11,g13)
    c: PointOnObject(g12,g13)
    c: Coincident(g13,g-1)
    c: PointOnObject(g12,g6)
    c: PointOnObject(g7,g-2)
    c: Horizontal(g5)
    c: Radius(g6) = 7.5
    c: Coincident(g14,g15)
    c: Coincident(g15,g16)
    c: Coincident(g16,g17)
    c: Coincident(g17,g18)
    c: Coincident(g18,g19)
    c: Coincident(g19,g14)
    c: Equal(g14, g15-g19) x5
    c: PointOnObject(g14,g20)
    c: PointOnObject(g15,g20)
    c: PointOnObject(g16,g20)
    c: PointOnObject(g17,g20)
    c: PointOnObject(g18,g20)
    c: PointOnObject(g19,g20)
    c: Coincident(g20,g-1)
    c: PointOnObject(g19,g-2)
    c: Radius(g20) = 10.5
    c: Coincident(g21,g22)
    c: Coincident(g22,g23)
    c: Coincident(g23,g24)
    c: Coincident(g24,g25)
    c: Coincident(g25,g26)
    c: Coincident(g26,g21)
    c: Equal(g21, g22-g26) x5
    c: PointOnObject(g21,g27)
    c: PointOnObject(g22,g27)
    c: PointOnObject(g23,g27)
    c: PointOnObject(g24,g27)
    c: PointOnObject(g25,g27)
    c: PointOnObject(g26,g27)
    c: Coincident(g27,g-1)
    c: PointOnObject(g26,g-2)
    c: Radius(g27) = 13.5
    c: Coincident(g28,g21)
    c: Coincident(g29,g25)
    c: Coincident(g30,g24)
    c: Coincident(g31,g23)
    c: Coincident(g32,g22)
    c: Coincident(g33,g21)
    c: Coincident(g34,g0)
    c: Coincident(g35,g34)
    c: Coincident(g36,g4)
    c: Coincident(g37,g36)
    c: Coincident(g38,g3)
    c: Coincident(g39,g38)
    c: Coincident(g40,g2)
    c: Coincident(g41,g40)
    c: Coincident(g42,g1)
    c: Coincident(g43,g42)
    c: Coincident(g44,g0)
    c: Coincident(g45,g44)
    c: Tangent(g35,g28) = 1.5708
    c: Tangent(g36,g28) = 1.5708
    c: Tangent(g37,g29) = 1.5708
    c: Tangent(g38,g29) = 1.5708
    c: Tangent(g39,g30) = 1.5708
    c: Tangent(g40,g30) = 1.5708
    c: Tangent(g41,g31) = 1.5708
    c: Tangent(g42,g31) = 1.5708
    c: Tangent(g43,g32) = 1.5708
    c: Tangent(g44,g32) = 1.5708
    c: Tangent(g45,g33) = 1.5708
    c: Tangent(g34,g33) = 1.5708
    c: Radius(g29) = 2.5
    c: Equal(g29,g28)
    c: Equal(g28,g33)
    c: Equal(g33,g32)
    c: Equal(g32,g31)
    c: Equal(g31,g30)
    c: Coincident(g46,g33)
    c: Coincident(g47,g14)
    c: Coincident(g48,g7)
    c: Coincident(g49,g28)
    c: Coincident(g50,g14)
    c: Coincident(g51,g7)
    c: Coincident(g52,g29)
    c: Coincident(g53,g18)
    c: Coincident(g54,g11)
    c: Coincident(g55,g30)
    c: Coincident(g56,g17)
    c: Coincident(g57,g10)
    c: Coincident(g58,g9)
    c: Coincident(g59,g16)
    c: Coincident(g60,g31)
    c: Coincident(g61,g32)
    c: Coincident(g62,g15)
    c: Coincident(g63,g8)
    c: Equal(g61,g62)
    c: Equal(g62,g63)
    c: Equal(g63,g58)
    c: Equal(g58,g59)
    c: Equal(g59,g60)
    c: Equal(g60,g55)
    c: Equal(g55,g56)
    c: Equal(g56,g57)
    c: Equal(g57,g54)
    c: Equal(g54,g53)
    c: Equal(g53,g52)
    c: Equal(g52,g51)
    c: Equal(g51,g50)
    c: Equal(g50,g49)
    c: Equal(g49,g46)
    c: Equal(g46,g47)
    c: Equal(g47,g48)
    c: Radius(g55) = 0.75
FEATURE [PartDesign::Pad] Pad298
  Length = 2
  Length2 = 100
  Profile = -> Sketch719
  Type = 0
FEATURE [Sketcher::SketchObject] Sketch714
  MapMode = 5
  Placement = pos=(0,0,2) rot=(0,0,1;0rad)
  Support = -> [Pad298]
  sketch-geometry (2):
    g0: Circle CenterX=0 CenterY=0 CenterZ=0 NormalX=0 NormalY=0 NormalZ=1 AngleXU=0 Radius=5
    g1: Circle CenterX=0 CenterY=0 CenterZ=0 NormalX=0 NormalY=0 NormalZ=1 AngleXU=0 Radius=3.5
  constraints (4):
    c: Coincident(g0,g-1)
    c: Coincident(g1,g0)
    c: Radius(g1) = 3.5
    c: Radius(g0) = 5
FEATURE [PartDesign::Pocket] Pocket289
  BaseFeature = -> Pad298
  Length = 1
  Length2 = 100
  Profile = -> Sketch714
  Type = 0
FEATURE [Sketcher::SketchObject] Sketch720
  MapMode = 5
  Placement = pos=(0,0,2) rot=(0,0,1;0rad)
  Support = -> [Pocket289]
  sketch-geometry (1):
    g0: Circle CenterX=0 CenterY=0 CenterZ=0 NormalX=0 NormalY=0 NormalZ=1 AngleXU=0 Radius=3
  constraints (2):
    c: Coincident(g0,g-1)
    c: Radius(g0) = 3
FEATURE [PartDesign::Pocket] Pocket284
  BaseFeature = -> Pocket289
  Length = 1
  Length2 = 100
  Profile = -> Sketch720
  Type = 0
FEATURE [Sketcher::SketchObject] Sketch713
  MapMode = 5
  Placement = pos=(0,0,1) rot=(0,0,1;0rad)
  Support = -> [Pocket284]
  sketch-geometry (1):
    g0: Circle CenterX=0 CenterY=0 CenterZ=0 NormalX=0 NormalY=0 NormalZ=1 AngleXU=0 Radius=1.5
  constraints (2):
    c: Coincident(g0,g-1)
    c: Radius(g0) = 1.5
FEATURE [PartDesign::Pocket] Pocket286
  BaseFeature = -> Pocket284
  Length = 5
  Length2 = 100
  Profile = -> Sketch713
  Type = 0
FEATURE [Sketcher::SketchObject] Sketch715
  MapMode = 5
  Placement = pos=(0,0,0) rot=(1,0,0;3.14159rad)
  Support = -> [Pocket286]
  sketch-geometry (2):
    g0: Circle CenterX=0 CenterY=0 CenterZ=0 NormalX=0 NormalY=0 NormalZ=1 AngleXU=0 Radius=4.5
    g1: Circle CenterX=0 CenterY=0 CenterZ=0 NormalX=0 NormalY=0 NormalZ=1 AngleXU=0 Radius=3
  constraints (4):
    c: Coincident(g0,g-1)
    c: Coincident(g1,g0)
    c: Radius(g0) = 4.5
    c: Radius(g1) = 3
FEATURE [PartDesign::Pad] Pad301
  BaseFeature = -> Pocket286
  Length = 3
  Length2 = 100
  Profile = -> Sketch715
  Type = 0
FEATURE [Sketcher::SketchObject] Sketch723
  MapMode = 5
  Support = -> [XY_Plane258]
  sketch-geometry (1):
    g0: Circle CenterX=0 CenterY=0 CenterZ=0 NormalX=0 NormalY=0 NormalZ=1 AngleXU=0 Radius=1.9
  constraints (2):
    c: Coincident(g0,g-1)
    c: Radius(g0) = 1.9
FEATURE [Sketcher::SketchObject] Sketch727
  MapMode = 5
  Support = -> [XY_Plane254]
  sketch-geometry (9):
    g0: ArcOfCircle CenterX=0 CenterY=0 CenterZ=0 NormalX=0 NormalY=0 NormalZ=1 AngleXU=0 Radius=16.5 StartAngle=2.61799 EndAngle=5.75959
    g1: LineSegment StartX=-14.2894 StartY=8.25 StartZ=0 EndX=-1.3577 EndY=30.6484 EndZ=0
    g2: ArcOfCircle CenterX=23.5 CenterY=16.2968 CenterZ=0 NormalX=0 NormalY=0 NormalZ=1 AngleXU=0 Radius=28.7032 StartAngle=1.5708 EndAngle=2.61799
    g3: LineSegment StartX=23.5 StartY=45 StartZ=0 EndX=40 EndY=45 EndZ=0
    g4: LineSegment StartX=40 StartY=45 StartZ=0 EndX=40 EndY=15 EndZ=0
    g5: LineSegment StartX=40 StartY=15 StartZ=0 EndX=28.6962 EndY=15 EndZ=0
    g6: ArcOfCircle CenterX=28.6962 CenterY=13.2968 CenterZ=0 NormalX=0 NormalY=0 NormalZ=1 AngleXU=0 Radius=1.70319 StartAngle=1.5708 EndAngle=2.61799
    g7: LineSegment StartX=27.2211 StartY=14.1484 StartZ=0 EndX=14.2894 EndY=-8.25 EndZ=0
    g8: LineSegment [constr] StartX=-1.3577 StartY=30.6484 StartZ=0 EndX=27.2211 EndY=14.1484 EndZ=0
  constraints (21):
    c: Tangent(g0,g1) = 1.5708
    c: Tangent(g1,g2) = 1.5708
    c: Tangent(g2,g3) = 1.5708
    c: Perpendicular(g3,g4) = 4.71239
    c: Coincident(g4,g5)
    c: Horizontal(g5)
    c: Tangent(g5,g6) = -1.5708
    c: Tangent(g6,g7) = -1.5708
    c: Parallel(g7,g1)
    c: Radius(g0) = 16.5
    c: Horizontal(g3)
    c: DistanceY(g4,g4) = 30
    c: Tangent(g7,g0) = 1.5708
    c: DistanceX(g0,g4) = 40
    c: Coincident(g8,g1)
    c: Coincident(g8,g6)
    c: Perpendicular(g1,g8)
    c: DistanceX(g3,g3) = 16.5
    c: DistanceY(g0,g4) = 15
    c: Angle(g8) = -0.523599
    c: Coincident(g0,g-1)
FEATURE [Sketcher::SketchObject] Sketch728
  MapMode = 5
  Support = -> [XY_Plane256]
FEATURE [Sketcher::SketchObject] Sketch729
  MapMode = 5
  Support = -> [XY_Plane257]
  sketch-geometry (1):
    g0: Circle CenterX=0 CenterY=0 CenterZ=0 NormalX=0 NormalY=0 NormalZ=1 AngleXU=0 Radius=1.9
  constraints (2):
    c: Coincident(g0,g-1)
    c: Radius(g0) = 1.9
FEATURE [PartDesign::Pad] Pad294  label="M3x8 Head035"
  Length = 2
  Length2 = 100
  Profile = -> Sketch729
  Type = 0
FEATURE [Sketcher::SketchObject] Sketch730
  MapMode = 5
  Support = -> [XY_Plane238]
  sketch-geometry (1):
    g0: Circle CenterX=0 CenterY=0 CenterZ=0 NormalX=0 NormalY=0 NormalZ=1 AngleXU=0 Radius=1.9
  constraints (2):
    c: Coincident(g0,g-1)
    c: Radius(g0) = 1.9
FEATURE [Sketcher::SketchObject] Sketch732
  MapMode = 5
  Support = -> [XY_Plane241]
FEATURE [Sketcher::SketchObject] Sketch733
  MapMode = 5
  Support = -> [XY_Plane241]
FEATURE [Sketcher::SketchObject] Sketch734
  MapMode = 5
  Support = -> [XY_Plane256]
  sketch-geometry (8):
    g0: LineSegment StartX=0 StartY=2.3094 StartZ=0 EndX=-2 EndY=1.1547 EndZ=0
    g1: LineSegment StartX=-2 StartY=1.1547 StartZ=0 EndX=-2 EndY=-1.1547 EndZ=0
    g2: LineSegment StartX=-2 StartY=-1.1547 StartZ=0 EndX=-2e-16 EndY=-2.3094 EndZ=0
    g3: LineSegment StartX=-2e-16 StartY=-2.3094 StartZ=0 EndX=2 EndY=-1.1547 EndZ=0
    g4: LineSegment StartX=2 StartY=-1.1547 StartZ=0 EndX=2 EndY=1.1547 EndZ=0
    g5: LineSegment StartX=2 StartY=1.1547 StartZ=0 EndX=0 EndY=2.3094 EndZ=0
    g6: Circle [constr] CenterX=0 CenterY=0 CenterZ=0 NormalX=0 NormalY=0 NormalZ=1 AngleXU=0 Radius=2.3094
    g7: Circle CenterX=0 CenterY=0 CenterZ=0 NormalX=0 NormalY=0 NormalZ=1 AngleXU=0 Radius=1
  constraints (18):
    c: Coincident(g0,g1)
    c: Coincident(g1,g2)
    c: Coincident(g2,g3)
    c: Coincident(g3,g4)
    c: Coincident(g4,g5)
    c: Coincident(g5,g0)
    c: Equal(g0, g1-g5) x5
    c: PointOnObject(g0,g6)
    c: PointOnObject(g1,g6)
    c: PointOnObject(g2,g6)
    c: PointOnObject(g3,g6)
    c: PointOnObject(g4,g6)
    c: PointOnObject(g5,g6)
    c: Coincident(g6,g-1)
    c: PointOnObject(g5,g-2)
    c: DistanceX(g0,g4) = 4
    c: Coincident(g7,g-1)
    c: Radius(g7) = 1
FEATURE [Sketcher::SketchObject] Sketch735
  MapMode = 5
  Support = -> [XY_Plane242]
  sketch-geometry (8):
    g0: LineSegment StartX=0 StartY=2.3094 StartZ=0 EndX=-2 EndY=1.1547 EndZ=0
    g1: LineSegment StartX=-2 StartY=1.1547 StartZ=0 EndX=-2 EndY=-1.1547 EndZ=0
    g2: LineSegment StartX=-2 StartY=-1.1547 StartZ=0 EndX=-2e-16 EndY=-2.3094 EndZ=0
    g3: LineSegment StartX=-2e-16 StartY=-2.3094 StartZ=0 EndX=2 EndY=-1.1547 EndZ=0
    g4: LineSegment StartX=2 StartY=-1.1547 StartZ=0 EndX=2 EndY=1.1547 EndZ=0
    g5: LineSegment StartX=2 StartY=1.1547 StartZ=0 EndX=0 EndY=2.3094 EndZ=0
    g6: Circle [constr] CenterX=0 CenterY=0 CenterZ=0 NormalX=0 NormalY=0 NormalZ=1 AngleXU=0 Radius=2.3094
    g7: Circle CenterX=0 CenterY=0 CenterZ=0 NormalX=0 NormalY=0 NormalZ=1 AngleXU=0 Radius=1
  constraints (18):
    c: Coincident(g0,g1)
    c: Coincident(g1,g2)
    c: Coincident(g2,g3)
    c: Coincident(g3,g4)
    c: Coincident(g4,g5)
    c: Coincident(g5,g0)
    c: Equal(g0, g1-g5) x5
    c: PointOnObject(g0,g6)
    c: PointOnObject(g1,g6)
    c: PointOnObject(g2,g6)
    c: PointOnObject(g3,g6)
    c: PointOnObject(g4,g6)
    c: PointOnObject(g5,g6)
    c: Coincident(g6,g-1)
    c: PointOnObject(g5,g-2)
    c: DistanceX(g0,g4) = 4
    c: Coincident(g7,g-1)
    c: Radius(g7) = 1
FEATURE [PartDesign::Pad] Pad295  label="M3 Nut Primitive056"
  Length = 0.6
  Length2 = 0.6
  Profile = -> Sketch735
  Type = 4
FEATURE [Sketcher::SketchObject] Sketch731
  ExternalGeometry = -> [Pad295]
  MapMode = 5
  Placement = pos=(0,0,0) rot=(0.57735,0.57735,0.57735;2.0944rad)
  Support = -> [YZ_Plane239]
  sketch-geometry (6):
    g0: LineSegment StartX=-1.9594 StartY=0.6 StartZ=0 EndX=-2.8094 EndY=0.6 EndZ=0
    g1: LineSegment StartX=-2.8094 StartY=0.6 StartZ=0 EndX=-2.8094 EndY=-0.6 EndZ=0
    g2: LineSegment StartX=-2.8094 StartY=-0.6 StartZ=0 EndX=-1.9594 EndY=-0.6 EndZ=0
    g3: LineSegment StartX=-1.9594 StartY=-0.6 StartZ=0 EndX=-2.3094 EndY=-0.4 EndZ=0
    g4: LineSegment StartX=-2.3094 StartY=-0.4 StartZ=0 EndX=-2.3094 EndY=0.4 EndZ=0
    g5: LineSegment StartX=-2.3094 StartY=0.4 StartZ=0 EndX=-1.9594 EndY=0.6 EndZ=0
  constraints (15):
    c: Horizontal(g0)
    c: Coincident(g0,g1)
    c: Coincident(g1,g2)
    c: Coincident(g2,g3)
    c: Coincident(g3,g4)
    c: Coincident(g4,g5)
    c: Coincident(g5,g0)
    c: Symmetric(g4,g3,g-1)
    c: Symmetric(g0,g2,g-1)
    c: Symmetric(g1,g0,g-1)
    c: DistanceX(g0,g4) = 0.5
    c: DistanceY(g3,g4) = 0.8
    c: DistanceY(g1,g0) = 1.2
    c: PointOnObject(g3,g-3)
    c: DistanceX(g4,g0) = 0.35
FEATURE [Sketcher::SketchObject] Sketch736
  MapMode = 5
  Support = -> [XY_Plane261]
  sketch-geometry (8):
    g0: LineSegment StartX=0 StartY=2.3094 StartZ=0 EndX=-2 EndY=1.1547 EndZ=0
    g1: LineSegment StartX=-2 StartY=1.1547 StartZ=0 EndX=-2 EndY=-1.1547 EndZ=0
    g2: LineSegment StartX=-2 StartY=-1.1547 StartZ=0 EndX=-2e-16 EndY=-2.3094 EndZ=0
    g3: LineSegment StartX=-2e-16 StartY=-2.3094 StartZ=0 EndX=2 EndY=-1.1547 EndZ=0
    g4: LineSegment StartX=2 StartY=-1.1547 StartZ=0 EndX=2 EndY=1.1547 EndZ=0
    g5: LineSegment StartX=2 StartY=1.1547 StartZ=0 EndX=0 EndY=2.3094 EndZ=0
    g6: Circle [constr] CenterX=0 CenterY=0 CenterZ=0 NormalX=0 NormalY=0 NormalZ=1 AngleXU=0 Radius=2.3094
    g7: Circle CenterX=0 CenterY=0 CenterZ=0 NormalX=0 NormalY=0 NormalZ=1 AngleXU=0 Radius=1
  constraints (18):
    c: Coincident(g0,g1)
    c: Coincident(g1,g2)
    c: Coincident(g2,g3)
    c: Coincident(g3,g4)
    c: Coincident(g4,g5)
    c: Coincident(g5,g0)
    c: Equal(g0, g1-g5) x5
    c: PointOnObject(g0,g6)
    c: PointOnObject(g1,g6)
    c: PointOnObject(g2,g6)
    c: PointOnObject(g3,g6)
    c: PointOnObject(g4,g6)
    c: PointOnObject(g5,g6)
    c: Coincident(g6,g-1)
    c: PointOnObject(g5,g-2)
    c: DistanceX(g0,g4) = 4
    c: Coincident(g7,g-1)
    c: Radius(g7) = 1
FEATURE [Sketcher::SketchObject] Sketch739
  MapMode = 5
  Support = -> [XY_Plane242]
FEATURE [Sketcher::SketchObject] Sketch740
  MapMode = 5
  Support = -> [XY_Plane242]
FEATURE [Sketcher::SketchObject] Sketch746
  MapMode = 5
  Support = -> [XY_Plane241]
  sketch-geometry (8):
    g0: LineSegment StartX=0 StartY=2.3094 StartZ=0 EndX=-2 EndY=1.1547 EndZ=0
    g1: LineSegment StartX=-2 StartY=1.1547 StartZ=0 EndX=-2 EndY=-1.1547 EndZ=0
    g2: LineSegment StartX=-2 StartY=-1.1547 StartZ=0 EndX=-2e-16 EndY=-2.3094 EndZ=0
    g3: LineSegment StartX=-2e-16 StartY=-2.3094 StartZ=0 EndX=2 EndY=-1.1547 EndZ=0
    g4: LineSegment StartX=2 StartY=-1.1547 StartZ=0 EndX=2 EndY=1.1547 EndZ=0
    g5: LineSegment StartX=2 StartY=1.1547 StartZ=0 EndX=0 EndY=2.3094 EndZ=0
    g6: Circle [constr] CenterX=0 CenterY=0 CenterZ=0 NormalX=0 NormalY=0 NormalZ=1 AngleXU=0 Radius=2.3094
    g7: Circle CenterX=0 CenterY=0 CenterZ=0 NormalX=0 NormalY=0 NormalZ=1 AngleXU=0 Radius=1
  constraints (18):
    c: Coincident(g0,g1)
    c: Coincident(g1,g2)
    c: Coincident(g2,g3)
    c: Coincident(g3,g4)
    c: Coincident(g4,g5)
    c: Coincident(g5,g0)
    c: Equal(g0, g1-g5) x5
    c: PointOnObject(g0,g6)
    c: PointOnObject(g1,g6)
    c: PointOnObject(g2,g6)
    c: PointOnObject(g3,g6)
    c: PointOnObject(g4,g6)
    c: PointOnObject(g5,g6)
    c: Coincident(g6,g-1)
    c: PointOnObject(g5,g-2)
    c: DistanceX(g0,g4) = 4
    c: Coincident(g7,g-1)
    c: Radius(g7) = 1
FEATURE [PartDesign::Pad] Pad296  label="M3 Nut Primitive057"
  Length = 0.6
  Length2 = 0.6
  Profile = -> Sketch746
  Type = 4
FEATURE [Sketcher::SketchObject] Sketch737
  ExternalGeometry = -> [Pad296]
  MapMode = 5
  Placement = pos=(0,0,0) rot=(0.57735,0.57735,0.57735;2.0944rad)
  Support = -> [YZ_Plane242]
  sketch-geometry (6):
    g0: LineSegment StartX=-1.9594 StartY=0.6 StartZ=0 EndX=-2.8094 EndY=0.6 EndZ=0
    g1: LineSegment StartX=-2.8094 StartY=0.6 StartZ=0 EndX=-2.8094 EndY=-0.6 EndZ=0
    g2: LineSegment StartX=-2.8094 StartY=-0.6 StartZ=0 EndX=-1.9594 EndY=-0.6 EndZ=0
    g3: LineSegment StartX=-1.9594 StartY=-0.6 StartZ=0 EndX=-2.3094 EndY=-0.4 EndZ=0
    g4: LineSegment StartX=-2.3094 StartY=-0.4 StartZ=0 EndX=-2.3094 EndY=0.4 EndZ=0
    g5: LineSegment StartX=-2.3094 StartY=0.4 StartZ=0 EndX=-1.9594 EndY=0.6 EndZ=0
  constraints (15):
    c: Horizontal(g0)
    c: Coincident(g0,g1)
    c: Coincident(g1,g2)
    c: Coincident(g2,g3)
    c: Coincident(g3,g4)
    c: Coincident(g4,g5)
    c: Coincident(g5,g0)
    c: Symmetric(g4,g3,g-1)
    c: Symmetric(g0,g2,g-1)
    c: Symmetric(g1,g0,g-1)
    c: DistanceX(g0,g4) = 0.5
    c: DistanceY(g3,g4) = 0.8
    c: DistanceY(g1,g0) = 1.2
    c: PointOnObject(g3,g-3)
    c: DistanceX(g4,g0) = 0.35
FEATURE [Sketcher::SketchObject] Sketch747
  MapMode = 5
  Support = -> [XY_Plane248]
  sketch-geometry (1):
    g0: Circle CenterX=0 CenterY=0 CenterZ=0 NormalX=0 NormalY=0 NormalZ=1 AngleXU=0 Radius=1.9
  constraints (2):
    c: Coincident(g0,g-1)
    c: Radius(g0) = 1.9
FEATURE [PartDesign::Pad] Pad297  label="M3x8 Head036"
  Length = 2
  Length2 = 100
  Profile = -> Sketch747
  Type = 0
FEATURE [Sketcher::SketchObject] Sketch748
  MapMode = 5
  Placement = pos=(0,0,2) rot=(0,0,1;0rad)
  Support = -> [Pad297]
  sketch-geometry (1):
    g0: Circle CenterX=0 CenterY=0 CenterZ=0 NormalX=0 NormalY=0 NormalZ=1 AngleXU=0 Radius=1
  constraints (2):
    c: Coincident(g0,g-1)
    c: Radius(g0) = 1
FEATURE [PartDesign::Pad] Pad299  label="M3x8 Thread035"
  BaseFeature = -> Pad297
  Length = 8
  Length2 = 100
  Profile = -> Sketch748
  Type = 0
FEATURE [Sketcher::SketchObject] Sketch749
  MapMode = 5
  Support = -> [XY_Plane255]
  sketch-geometry (1):
    g0: Circle CenterX=0 CenterY=0 CenterZ=0 NormalX=0 NormalY=0 NormalZ=1 AngleXU=0 Radius=1.9
  constraints (2):
    c: Coincident(g0,g-1)
    c: Radius(g0) = 1.9
FEATURE [Sketcher::SketchObject] Sketch750
  MapMode = 5
  Placement = pos=(0,0,2) rot=(0,0,1;0rad)
  Support = -> [Pad294]
  sketch-geometry (1):
    g0: Circle CenterX=0 CenterY=0 CenterZ=0 NormalX=0 NormalY=0 NormalZ=1 AngleXU=0 Radius=1
  constraints (2):
    c: Coincident(g0,g-1)
    c: Radius(g0) = 1
FEATURE [Sketcher::SketchObject] Sketch751
  MapMode = 5
  Support = -> [XY_Plane249]
  sketch-geometry (8):
    g0: LineSegment StartX=0 StartY=2.3094 StartZ=0 EndX=-2 EndY=1.1547 EndZ=0
    g1: LineSegment StartX=-2 StartY=1.1547 StartZ=0 EndX=-2 EndY=-1.1547 EndZ=0
    g2: LineSegment StartX=-2 StartY=-1.1547 StartZ=0 EndX=-2e-16 EndY=-2.3094 EndZ=0
    g3: LineSegment StartX=-2e-16 StartY=-2.3094 StartZ=0 EndX=2 EndY=-1.1547 EndZ=0
    g4: LineSegment StartX=2 StartY=-1.1547 StartZ=0 EndX=2 EndY=1.1547 EndZ=0
    g5: LineSegment StartX=2 StartY=1.1547 StartZ=0 EndX=0 EndY=2.3094 EndZ=0
    g6: Circle [constr] CenterX=0 CenterY=0 CenterZ=0 NormalX=0 NormalY=0 NormalZ=1 AngleXU=0 Radius=2.3094
    g7: Circle CenterX=0 CenterY=0 CenterZ=0 NormalX=0 NormalY=0 NormalZ=1 AngleXU=0 Radius=1
  constraints (18):
    c: Coincident(g0,g1)
    c: Coincident(g1,g2)
    c: Coincident(g2,g3)
    c: Coincident(g3,g4)
    c: Coincident(g4,g5)
    c: Coincident(g5,g0)
    c: Equal(g0, g1-g5) x5
    c: PointOnObject(g0,g6)
    c: PointOnObject(g1,g6)
    c: PointOnObject(g2,g6)
    c: PointOnObject(g3,g6)
    c: PointOnObject(g4,g6)
    c: PointOnObject(g5,g6)
    c: Coincident(g6,g-1)
    c: PointOnObject(g5,g-2)
    c: DistanceX(g0,g4) = 4
    c: Coincident(g7,g-1)
    c: Radius(g7) = 1
FEATURE [Sketcher::SketchObject] Sketch752
  MapMode = 5
  Placement = pos=(0,0,0) rot=(1,0,0;3.14159rad)
  Support = -> [Pad299]
  sketch-geometry (7):
    g0: LineSegment StartX=0.77 StartY=0.44456 StartZ=0 EndX=0 EndY=0.889119 EndZ=0
    g1: LineSegment StartX=0 StartY=0.889119 StartZ=0 EndX=-0.77 EndY=0.44456 EndZ=0
    g2: LineSegment StartX=-0.77 StartY=0.44456 StartZ=0 EndX=-0.77 EndY=-0.44456 EndZ=0
    g3: LineSegment StartX=-0.77 StartY=-0.44456 StartZ=0 EndX=3.85628e-11 EndY=-0.889119 EndZ=0
    g4: LineSegment StartX=3.85628e-11 StartY=-0.889119 StartZ=0 EndX=0.77 EndY=-0.44456 EndZ=0
    g5: LineSegment StartX=0.77 StartY=-0.44456 StartZ=0 EndX=0.77 EndY=0.44456 EndZ=0
    g6: Circle [constr] CenterX=0 CenterY=0 CenterZ=0 NormalX=0 NormalY=0 NormalZ=1 AngleXU=0 Radius=0.889119
  constraints (16):
    c: Coincident(g0,g1)
    c: Coincident(g1,g2)
    c: Coincident(g2,g3)
    c: Coincident(g3,g4)
    c: Coincident(g4,g5)
    c: Coincident(g5,g0)
    c: Equal(g0, g1-g5) x5
    c: PointOnObject(g0,g6)
    c: PointOnObject(g1,g6)
    c: PointOnObject(g2,g6)
    c: PointOnObject(g3,g6)
    c: PointOnObject(g4,g6)
    c: PointOnObject(g5,g6)
    c: Coincident(g6,g-1)
    c: PointOnObject(g0,g-2)
    c: DistanceX(g1,g0) = 1.54
FEATURE [PartDesign::Pocket] Pocket285  label="M3x8 Wrench035"
  BaseFeature = -> Pad299
  Length = 1
  Length2 = 100
  Profile = -> Sketch752
  Type = 0
FEATURE [PartDesign::Chamfer] Chamfer132  label="M3x8 Smooth035"
  Base = -> Pocket285 [Face11,Edge2,Edge24,Edge3]
  BaseFeature = -> Pocket285
  Size = 0.2
FEATURE [PartDesign::Body] Body174  label="M2x034"
  Group = -> [Sketch747,Pad297,Sketch748,Pad299,Sketch752,Pocket285,Chamfer132]
  Origin = -> Origin256
  Tip = -> Chamfer132
FEATURE [Sketcher::SketchObject] Sketch755
  MapMode = 5
  Support = -> [XY_Plane261]
FEATURE [Sketcher::SketchObject] Sketch756
  MapMode = 5
  Support = -> [XY_Plane249]
FEATURE [Sketcher::SketchObject] Sketch757
  MapMode = 5
  Support = -> [XY_Plane251]
  sketch-geometry (8):
    g0: LineSegment StartX=0 StartY=2.3094 StartZ=0 EndX=-2 EndY=1.1547 EndZ=0
    g1: LineSegment StartX=-2 StartY=1.1547 StartZ=0 EndX=-2 EndY=-1.1547 EndZ=0
    g2: LineSegment StartX=-2 StartY=-1.1547 StartZ=0 EndX=-2e-16 EndY=-2.3094 EndZ=0
    g3: LineSegment StartX=-2e-16 StartY=-2.3094 StartZ=0 EndX=2 EndY=-1.1547 EndZ=0
    g4: LineSegment StartX=2 StartY=-1.1547 StartZ=0 EndX=2 EndY=1.1547 EndZ=0
    g5: LineSegment StartX=2 StartY=1.1547 StartZ=0 EndX=0 EndY=2.3094 EndZ=0
    g6: Circle [constr] CenterX=0 CenterY=0 CenterZ=0 NormalX=0 NormalY=0 NormalZ=1 AngleXU=0 Radius=2.3094
    g7: Circle CenterX=0 CenterY=0 CenterZ=0 NormalX=0 NormalY=0 NormalZ=1 AngleXU=0 Radius=1
  constraints (18):
    c: Coincident(g0,g1)
    c: Coincident(g1,g2)
    c: Coincident(g2,g3)
    c: Coincident(g3,g4)
    c: Coincident(g4,g5)
    c: Coincident(g5,g0)
    c: Equal(g0, g1-g5) x5
    c: PointOnObject(g0,g6)
    c: PointOnObject(g1,g6)
    c: PointOnObject(g2,g6)
    c: PointOnObject(g3,g6)
    c: PointOnObject(g4,g6)
    c: PointOnObject(g5,g6)
    c: Coincident(g6,g-1)
    c: PointOnObject(g5,g-2)
    c: DistanceX(g0,g4) = 4
    c: Coincident(g7,g-1)
    c: Radius(g7) = 1
FEATURE [Sketcher::SketchObject] Sketch759
  MapMode = 5
  Support = -> [XY_Plane249]
FEATURE [Sketcher::SketchObject] Sketch766
  MapMode = 5
  Support = -> [XY_Plane261]
FEATURE [Sketcher::SketchObject] Sketch768
  MapMode = 5
  Support = -> [XY_Plane251]
FEATURE [Sketcher::SketchObject] Sketch770
  MapMode = 5
  Support = -> [XY_Plane253]
  sketch-geometry (1):
    g0: Circle CenterX=0 CenterY=0 CenterZ=0 NormalX=0 NormalY=0 NormalZ=1 AngleXU=0 Radius=1.9
  constraints (2):
    c: Coincident(g0,g-1)
    c: Radius(g0) = 1.9
FEATURE [Sketcher::SketchObject] Sketch772
  MapMode = 5
  Support = -> [XY_Plane251]
FEATURE [Sketcher::SketchObject] Sketch775
  MapMode = 5
  Support = -> [XY_Plane260]
  sketch-geometry (9):
    g0: ArcOfCircle CenterX=0 CenterY=0 CenterZ=0 NormalX=0 NormalY=0 NormalZ=1 AngleXU=0 Radius=16.5 StartAngle=3.66519 EndAngle=6.80678
    g1: LineSegment StartX=-14.2894 StartY=-8.25 StartZ=0 EndX=-27.2211 EndY=14.1484 EndZ=0
    g2: LineSegment StartX=1.3577 StartY=30.6484 StartZ=0 EndX=14.2894 EndY=8.25 EndZ=0
    g3: LineSegment [constr] StartX=-27.2211 StartY=14.1484 StartZ=0 EndX=1.3577 EndY=30.6484 EndZ=0
    g4: ArcOfCircle CenterX=-28.6962 CenterY=13.2968 CenterZ=0 NormalX=0 NormalY=0 NormalZ=1 AngleXU=0 Radius=1.70319 StartAngle=0.523599 EndAngle=1.5708
    g5: ArcOfCircle CenterX=-23.5 CenterY=16.2968 CenterZ=0 NormalX=0 NormalY=0 NormalZ=1 AngleXU=0 Radius=28.7032 StartAngle=0.523599 EndAngle=1.5708
    g6: LineSegment StartX=-28.6962 StartY=15 StartZ=0 EndX=-40 EndY=15 EndZ=0
    g7: LineSegment StartX=-40 StartY=15 StartZ=0 EndX=-40 EndY=45 EndZ=0
    g8: LineSegment StartX=-40 StartY=45 StartZ=0 EndX=-23.5 EndY=45 EndZ=0
  constraints (22):
    c: Coincident(g0,g-1)
    c: Tangent(g0,g1) = 1.5708
    c: Coincident(g3,g2) = -1.5708
    c: Parallel(g2,g1)
    c: Radius(g0) = 16.5
    c: Tangent(g2,g0) = 1.5708
    c: Coincident(g3,g1)
    c: Perpendicular(g1,g3)
    c: Tangent(g5,g2) = 1.5708
    c: Tangent(g4,g1) = -1.5708
    c: Horizontal(g6)
    c: Coincident(g7,g6)
    c: Vertical(g7)
    c: Coincident(g8,g7)
    c: Horizontal(g8)
    c: Tangent(g6,g4) = -1.5708
    c: DistanceY(g7,g7) = 30
    c: DistanceX(g6,g0) = 40
    c: DistanceX(g8,g8) = 16.5
    c: Tangent(g8,g5) = 1.5708
    c: DistanceY(g0,g4) = 15
    c: Angle(g3) = 0.523599
FEATURE [Sketcher::SketchObject] Sketch782
  MapMode = 5
  Support = -> [XY_Plane267]
  sketch-geometry (1):
    g0: Circle CenterX=0 CenterY=0 CenterZ=0 NormalX=0 NormalY=0 NormalZ=1 AngleXU=0 Radius=2.75
  constraints (2):
    c: Coincident(g0,g-1)
    c: Radius(g0) = 2.75
FEATURE [Sketcher::SketchObject] Sketch783
  MapMode = 5
  Placement = pos=(0,0,0) rot=(1,0,0;1.5708rad)
  Support = -> [XZ_Plane257]
  sketch-geometry (1):
    g0: Circle CenterX=-1.55 CenterY=4 CenterZ=0 NormalX=0 NormalY=0 NormalZ=1 AngleXU=0 Radius=0.75
  constraints (3):
    c: Radius(g0) = 0.75
    c: DistanceY(g-1,g0) = 4
    c: DistanceX(g0,g-1) = 1.55
FEATURE [Sketcher::SketchObject] Sketch790
  MapMode = 5
  Support = -> [XY_Plane266]
  sketch-geometry (1):
    g0: Circle CenterX=0 CenterY=10.15 CenterZ=0 NormalX=0 NormalY=0 NormalZ=1 AngleXU=0 Radius=3
  constraints (3):
    c: PointOnObject(g0,g-2)
    c: DistanceY(g-1,g0) = 10.15
    c: Radius(g0) = 3
FEATURE [Sketcher::SketchObject] Sketch792
  MapMode = 5
  Support = -> [XY_Plane282]
  sketch-geometry (1):
    g0: Circle CenterX=0 CenterY=0 CenterZ=0 NormalX=0 NormalY=0 NormalZ=1 AngleXU=0 Radius=2.75
  constraints (2):
    c: Coincident(g0,g-1)
    c: Radius(g0) = 2.75
FEATURE [Sketcher::SketchObject] Sketch793
  MapMode = 5
  Support = -> [XY_Plane279]
  sketch-geometry (8):
    g0: LineSegment StartX=0 StartY=3.17543 StartZ=0 EndX=-2.75 EndY=1.58771 EndZ=0
    g1: LineSegment StartX=-2.75 StartY=1.58771 StartZ=0 EndX=-2.75 EndY=-1.58771 EndZ=0
    g2: LineSegment StartX=-2.75 StartY=-1.58771 StartZ=0 EndX=0 EndY=-3.17543 EndZ=0
    g3: LineSegment StartX=0 StartY=-3.17543 StartZ=0 EndX=2.75 EndY=-1.58771 EndZ=0
    g4: LineSegment StartX=2.75 StartY=-1.58771 StartZ=0 EndX=2.75 EndY=1.58771 EndZ=0
    g5: LineSegment StartX=2.75 StartY=1.58771 StartZ=0 EndX=0 EndY=3.17543 EndZ=0
    g6: Circle [constr] CenterX=0 CenterY=0 CenterZ=0 NormalX=0 NormalY=0 NormalZ=1 AngleXU=0 Radius=3.17543
    g7: Circle CenterX=0 CenterY=0 CenterZ=0 NormalX=0 NormalY=0 NormalZ=1 AngleXU=0 Radius=1.5
  constraints (18):
    c: Coincident(g0,g1)
    c: Coincident(g1,g2)
    c: Coincident(g2,g3)
    c: Coincident(g3,g4)
    c: Coincident(g4,g5)
    c: Coincident(g5,g0)
    c: Equal(g0, g1-g5) x5
    c: PointOnObject(g0,g6)
    c: PointOnObject(g1,g6)
    c: PointOnObject(g2,g6)
    c: PointOnObject(g3,g6)
    c: PointOnObject(g4,g6)
    c: PointOnObject(g5,g6)
    c: Coincident(g6,g-1)
    c: PointOnObject(g5,g-2)
    c: DistanceX(g0,g4) = 5.5
    c: Coincident(g7,g-1)
    c: Radius(g7) = 1.5
FEATURE [Sketcher::SketchObject] Sketch794
  MapMode = 5
  Support = -> [XY_Plane293]
  sketch-geometry (1):
    g0: Circle CenterX=0 CenterY=0 CenterZ=0 NormalX=0 NormalY=0 NormalZ=1 AngleXU=0 Radius=2.75
  constraints (2):
    c: Coincident(g0,g-1)
    c: Radius(g0) = 2.75
FEATURE [PartDesign::Groove] Groove059  label="M3 Nut Smooth057"
  Angle = 360
  Axis = (-2e-16,3e-16,1)
  Base = (0,0,0)
  BaseFeature = -> Pad296
  Profile = -> Sketch737
  ReferenceAxis = -> Sketch737 [V_Axis]
  Reversed = true
FEATURE [PartDesign::Chamfer] Chamfer173  label="M3 Nut Smooth Hole071"
  Base = -> Groove059 [Edge24,Edge23]
  BaseFeature = -> Groove059
  Size = 0.2
FEATURE [PartDesign::Body] Body182  label="M2 Nut032"
  Group = -> [Sketch746,Pad296,Sketch737,Groove059,Chamfer173,Sketch732,Sketch733]
  Origin = -> Origin250
  Placement = pos=(0,0,2.75) rot=(0,0,1;0rad)
  Tip = -> Chamfer173
FEATURE [PartDesign::Pad] Pad303  label="M3 Nut Primitive058"
  Length = 0.6
  Length2 = 0.6
  Profile = -> Sketch734
  Type = 4
FEATURE [Sketcher::SketchObject] Sketch724
  ExternalGeometry = -> [Pad303]
  MapMode = 5
  Placement = pos=(0,0,0) rot=(0.57735,0.57735,0.57735;2.0944rad)
  Support = -> [YZ_Plane260]
  sketch-geometry (6):
    g0: LineSegment StartX=-1.9594 StartY=0.6 StartZ=0 EndX=-2.8094 EndY=0.6 EndZ=0
    g1: LineSegment StartX=-2.8094 StartY=0.6 StartZ=0 EndX=-2.8094 EndY=-0.6 EndZ=0
    g2: LineSegment StartX=-2.8094 StartY=-0.6 StartZ=0 EndX=-1.9594 EndY=-0.6 EndZ=0
    g3: LineSegment StartX=-1.9594 StartY=-0.6 StartZ=0 EndX=-2.3094 EndY=-0.4 EndZ=0
    g4: LineSegment StartX=-2.3094 StartY=-0.4 StartZ=0 EndX=-2.3094 EndY=0.4 EndZ=0
    g5: LineSegment StartX=-2.3094 StartY=0.4 StartZ=0 EndX=-1.9594 EndY=0.6 EndZ=0
  constraints (15):
    c: Horizontal(g0)
    c: Coincident(g0,g1)
    c: Coincident(g1,g2)
    c: Coincident(g2,g3)
    c: Coincident(g3,g4)
    c: Coincident(g4,g5)
    c: Coincident(g5,g0)
    c: Symmetric(g4,g3,g-1)
    c: Symmetric(g0,g2,g-1)
    c: Symmetric(g1,g0,g-1)
    c: DistanceX(g0,g4) = 0.5
    c: DistanceY(g3,g4) = 0.8
    c: DistanceY(g1,g0) = 1.2
    c: PointOnObject(g3,g-3)
    c: DistanceX(g4,g0) = 0.35
FEATURE [PartDesign::Pad] Pad304  label="Baseplate013"
  Length = 5
  Length2 = 100
  Profile = -> Sketch727
  Type = 0
FEATURE [Sketcher::SketchObject] Sketch712
  MapMode = 5
  Placement = pos=(40,-9.6e-15,0) rot=(0.57735,0.57735,0.57735;2.0944rad)
  Support = -> [Pad304]
  sketch-geometry (4):
    g0: ArcOfCircle CenterX=35 CenterY=-21 CenterZ=0 NormalX=0 NormalY=0 NormalZ=1 AngleXU=0 Radius=26 StartAngle=1.17601 EndAngle=1.5708
    g1: LineSegment StartX=35 StartY=5 StartZ=0 EndX=35 EndY=6 EndZ=0
    g2: LineSegment StartX=35 StartY=6 StartZ=0 EndX=45 EndY=6 EndZ=0
    g3: LineSegment StartX=45 StartY=6 StartZ=0 EndX=45 EndY=3 EndZ=0
  constraints (13):
    c: Coincident(g1,g0)
    c: Vertical(g1)
    c: Horizontal(g2)
    c: Coincident(g3,g2)
    c: Vertical(g3)
    c: Coincident(g0,g3)
    c: Coincident(g1,g2)
    c: DistanceY(g1,g1) = 1
    c: DistanceY(g3,g3) = 3
    c: DistanceX(g2,g2) = 10
    c: DistanceY(g-1,g0) = 5
    c: DistanceX(g-1,g0) = 45
    c: Perpendicular(g0,g1)
FEATURE [PartDesign::SubtractivePipe] SubtractivePipe007  label="Smooth Surfaces004"
  AuxilleryCurvelinear = true
  AuxillerySpineTangent = false
  BaseFeature = -> Pad304
  Binormal = (0,0,0)
  Mode = 0
  Profile = -> Sketch712
  Spine = -> Pad304 [Edge19,Edge22,Edge24,Edge4,Edge7,Edge10,Edge13]
  SpineTangent = false
  Transformation = 0
  Transition = 0
FEATURE [Sketcher::SketchObject] Sketch722
  MapMode = 5
  Placement = pos=(0,0,5) rot=(0,0,1;0rad)
  Support = -> [SubtractivePipe007]
  sketch-geometry (3):
    g0: Circle [constr] CenterX=0 CenterY=15 CenterZ=0 NormalX=0 NormalY=0 NormalZ=1 AngleXU=0 Radius=35
    g1: Circle CenterX=28.7228 CenterY=35 CenterZ=0 NormalX=0 NormalY=0 NormalZ=1 AngleXU=0 Radius=2.85
    g2: Circle CenterX=33.541 CenterY=25 CenterZ=0 NormalX=0 NormalY=0 NormalZ=1 AngleXU=0 Radius=2.85
  constraints (9):
    c: PointOnObject(g1,g0)
    c: PointOnObject(g2,g0)
    c: Radius(g0) = 35
    c: Equal(g2,g1)
    c: Radius(g1) = 2.85
    c: DistanceY(g2,g1) = 10
    c: DistanceY(g-1,g0) = 15
    c: DistanceY(g0,g2) = 10
    c: DistanceX(g-1,g0) = 0
FEATURE [PartDesign::Fillet] Fillet096  label="Smooth Edges006"
  Base = -> SubtractivePipe007 [Edge21]
  BaseFeature = -> SubtractivePipe007
  Radius = 1.5
FEATURE [Sketcher::SketchObject] Sketch718
  MapMode = 5
  Placement = pos=(0,0,5) rot=(0,0,1;0rad)
  Support = -> [Fillet096]
  sketch-geometry (33):
    g0: LineSegment [constr] StartX=11.6913 StartY=6.75 StartZ=0 EndX=0 EndY=13.5 EndZ=0
    g1: LineSegment [constr] StartX=0 StartY=13.5 StartZ=0 EndX=-11.6913 EndY=6.75 EndZ=0
    g2: LineSegment [constr] StartX=-11.6913 StartY=6.75 StartZ=0 EndX=-11.6913 EndY=-6.75 EndZ=0
    g3: LineSegment [constr] StartX=-11.6913 StartY=-6.75 StartZ=0 EndX=0 EndY=-13.5 EndZ=0
    g4: LineSegment [constr] StartX=-6e-16 StartY=-13.5 StartZ=0 EndX=11.6913 EndY=-6.75 EndZ=0
    g5: LineSegment [constr] StartX=11.6913 StartY=-6.75 StartZ=0 EndX=11.6913 EndY=6.75 EndZ=0
    g6: Circle [constr] CenterX=0 CenterY=0 CenterZ=0 NormalX=0 NormalY=0 NormalZ=1 AngleXU=0 Radius=13.5
    g7: LineSegment [constr] StartX=7.5 StartY=9e-16 StartZ=0 EndX=3.75 EndY=6.49519 EndZ=0
    g8: LineSegment [constr] StartX=3.75 StartY=6.49519 StartZ=0 EndX=-3.75 EndY=6.49519 EndZ=0
    g9: LineSegment [constr] StartX=-3.75 StartY=6.49519 StartZ=0 EndX=-7.5 EndY=-9e-16 EndZ=0
    g10: LineSegment [constr] StartX=-7.5 StartY=-9e-16 StartZ=0 EndX=-3.75 EndY=-6.49519 EndZ=0
    g11: LineSegment [constr] StartX=-3.75 StartY=-6.49519 StartZ=0 EndX=3.75 EndY=-6.49519 EndZ=0
    g12: LineSegment [constr] StartX=3.75 StartY=-6.49519 StartZ=0 EndX=7.5 EndY=9e-16 EndZ=0
    g13: Circle [constr] CenterX=0 CenterY=0 CenterZ=0 NormalX=0 NormalY=0 NormalZ=1 AngleXU=0 Radius=7.5
    g14: ArcOfCircle CenterX=11.6913 CenterY=-6.75 CenterZ=0 NormalX=0 NormalY=0 NormalZ=1 AngleXU=0 Radius=2.6 StartAngle=4.34694 EndAngle=7.17223
    g15: ArcOfCircle CenterX=-6e-16 CenterY=-13.5 CenterZ=0 NormalX=0 NormalY=0 NormalZ=1 AngleXU=0 Radius=2.6 StartAngle=3.29974 EndAngle=6.12503
    g16: ArcOfCircle CenterX=-11.6913 CenterY=-6.75 CenterZ=0 NormalX=0 NormalY=0 NormalZ=1 AngleXU=0 Radius=2.6 StartAngle=2.25255 EndAngle=5.07784
    g17: ArcOfCircle CenterX=-11.6913 CenterY=6.75 CenterZ=0 NormalX=0 NormalY=0 NormalZ=1 AngleXU=0 Radius=2.6 StartAngle=1.20535 EndAngle=4.03064
    g18: ArcOfCircle CenterX=0 CenterY=13.5 CenterZ=0 NormalX=0 NormalY=0 NormalZ=1 AngleXU=0 Radius=2.6 StartAngle=0.15815 EndAngle=2.98344
    g19: ArcOfCircle CenterX=11.6913 CenterY=6.75 CenterZ=0 NormalX=0 NormalY=0 NormalZ=1 AngleXU=0 Radius=2.6 StartAngle=5.39414 EndAngle=8.21943
    g20: LineSegment StartX=13.3297 StartY=4.73117 StartZ=0 EndX=7.5 EndY=9e-16 EndZ=0
    g21: LineSegment StartX=7.5 StartY=9e-16 StartZ=0 EndX=13.3297 EndY=-4.73117 EndZ=0
    g22: LineSegment StartX=10.7622 StartY=-9.17831 StartZ=0 EndX=3.75 EndY=-6.49519 EndZ=0
    g23: LineSegment StartX=3.75 StartY=-6.49519 StartZ=0 EndX=2.56755 EndY=-13.9095 EndZ=0
    g24: LineSegment StartX=-2.56755 StartY=-13.9095 StartZ=0 EndX=-3.75 EndY=-6.49519 EndZ=0
    g25: LineSegment StartX=-3.75 StartY=-6.49519 StartZ=0 EndX=-10.7622 EndY=-9.17831 EndZ=0
    g26: LineSegment StartX=-13.3297 StartY=-4.73117 StartZ=0 EndX=-7.5 EndY=-9e-16 EndZ=0
    g27: LineSegment StartX=-7.5 StartY=-9e-16 StartZ=0 EndX=-13.3297 EndY=4.73117 EndZ=0
    g28: LineSegment StartX=-10.7622 StartY=9.17831 StartZ=0 EndX=-3.75 EndY=6.49519 EndZ=0
    g29: LineSegment StartX=-3.75 StartY=6.49519 StartZ=0 EndX=-2.56755 EndY=13.9095 EndZ=0
    g30: LineSegment StartX=2.56755 StartY=13.9095 StartZ=0 EndX=3.75 EndY=6.49519 EndZ=0
    g31: LineSegment StartX=3.75 StartY=6.49519 StartZ=0 EndX=10.7622 EndY=9.17831 EndZ=0
    g32: LineSegment [constr] StartX=11.6913 StartY=6.75 StartZ=0 EndX=-11.6913 EndY=-6.75 EndZ=0
  constraints (70):
    c: Coincident(g0,g1)
    c: Coincident(g1,g2)
    c: Coincident(g2,g3)
    c: Coincident(g3,g4)
    c: Coincident(g4,g5)
    c: Coincident(g5,g0)
    c: Equal(g0, g1-g5) x5
    c: PointOnObject(g0,g6)
    c: PointOnObject(g1,g6)
    c: PointOnObject(g2,g6)
    c: PointOnObject(g3,g6)
    c: PointOnObject(g4,g6)
    c: PointOnObject(g5,g6)
    c: Coincident(g6,g-1)
    c: Radius(g6) = 13.5
    c: Coincident(g7,g8)
    c: Coincident(g8,g9)
    c: Coincident(g9,g10)
    c: Coincident(g10,g11)
    c: Coincident(g11,g12)
    c: Coincident(g12,g7)
    c: Equal(g7, g8-g12) x5
    c: PointOnObject(g7,g13)
    c: PointOnObject(g8,g13)
    c: PointOnObject(g9,g13)
    c: PointOnObject(g10,g13)
    c: PointOnObject(g11,g13)
    c: PointOnObject(g12,g13)
    c: Coincident(g13,g-1)
    c: Radius(g13) = 7.5
    c: Coincident(g14,g4)
    c: Coincident(g15,g3)
    c: Coincident(g16,g2)
    c: Coincident(g17,g1)
    c: Coincident(g18,g0)
    c: Coincident(g19,g0)
    c: Coincident(g20,g7)
    c: Coincident(g21,g20)
    c: Coincident(g22,g11)
    c: Coincident(g23,g22)
    c: Coincident(g24,g10)
    c: Coincident(g25,g24)
    c: Coincident(g26,g9)
    c: Coincident(g28,g8)
    c: Coincident(g29,g28)
    c: Coincident(g30,g7)
    c: Coincident(g31,g30)
    c: Tangent(g22,g14) = 1.5708
    c: Tangent(g23,g15) = 1.5708
    c: Tangent(g24,g15) = 1.5708
    c: Tangent(g26,g16) = 1.5708
    c: Tangent(g21,g14) = 1.5708
    c: Tangent(g16,g25) = 1.5708
    c: Tangent(g29,g18) = 1.5708
    c: Tangent(g30,g18) = 1.5708
    c: Tangent(g31,g19) = 1.5708
    c: Tangent(g20,g19) = 1.5708
    c: Tangent(g27,g17) = 1.5708
    c: Tangent(g17,g28) = 1.5708
    c: Coincident(g27,g26)
    c: Equal(g14,g15)
    c: Equal(g15,g16)
    c: Equal(g16,g17)
    c: Equal(g17,g18)
    c: Equal(g18,g19)
    c: Radius(g14) = 2.6
    c: Coincident(g32,g19)
    c: Coincident(g32,g16)
    c: Perpendicular(g32,g7)
    c: PointOnObject(g18,g-2)
FEATURE [PartDesign::Pocket] Pocket293  label="Screwheads Montage003"
  BaseFeature = -> Fillet096
  Length = 3
  Length2 = 100
  Profile = -> Sketch722
  Type = 0
FEATURE [Sketcher::SketchObject] Sketch721
  MapMode = 5
  Placement = pos=(0,0,2) rot=(0,0,1;0rad)
  Support = -> [Pocket293]
  sketch-geometry (3):
    g0: Circle [constr] CenterX=0 CenterY=15 CenterZ=0 NormalX=0 NormalY=0 NormalZ=1 AngleXU=0 Radius=35
    g1: Circle CenterX=28.7228 CenterY=35 CenterZ=0 NormalX=0 NormalY=0 NormalZ=1 AngleXU=0 Radius=1.6
    g2: Circle CenterX=33.541 CenterY=25 CenterZ=0 NormalX=0 NormalY=0 NormalZ=1 AngleXU=0 Radius=1.6
  constraints (9):
    c: Radius(g0) = 35
    c: PointOnObject(g1,g0)
    c: PointOnObject(g2,g0)
    c: Equal(g2,g1)
    c: Radius(g2) = 1.6
    c: DistanceY(g2,g1) = 10
    c: DistanceY(g-1,g0) = 15
    c: DistanceY(g0,g2) = 10
    c: DistanceX(g-1,g0) = 0
FEATURE [PartDesign::Pocket] Pocket283  label="Screwholes Montage003"
  BaseFeature = -> Pocket293
  Length = 3
  Length2 = 100
  Profile = -> Sketch721
  Type = 0
FEATURE [PartDesign::Pocket] Pocket287  label="Servohorn007"
  BaseFeature = -> Pocket283
  Length = 2
  Length2 = 100
  Profile = -> Sketch718
  Type = 0
FEATURE [PartDesign::Fillet] Fillet088  label="Smooth Servhohorn Edges002"
  Base = -> Pocket287 [Edge124,Edge122,Edge129,Edge121,Edge136,Edge120]
  BaseFeature = -> Pocket287
  Radius = 1
FEATURE [Sketcher::SketchObject] Sketch717
  MapMode = 5
  Placement = pos=(0,0,3) rot=(0,0,1;0rad)
  Support = -> [Fillet088]
  sketch-geometry (14):
    g0: LineSegment [constr] StartX=0 StartY=10.5 StartZ=0 EndX=-9.09327 EndY=5.25 EndZ=0
    g1: LineSegment [constr] StartX=-9.09327 StartY=5.25 StartZ=0 EndX=-9.09327 EndY=-5.25 EndZ=0
    g2: LineSegment [constr] StartX=-9.09327 StartY=-5.25 StartZ=0 EndX=0 EndY=-10.5 EndZ=0
    g3: LineSegment [constr] StartX=0 StartY=-10.5 StartZ=0 EndX=9.09327 EndY=-5.25 EndZ=0
    g4: LineSegment [constr] StartX=9.09327 StartY=-5.25 StartZ=0 EndX=9.09327 EndY=5.25 EndZ=0
    g5: LineSegment [constr] StartX=9.09327 StartY=5.25 StartZ=0 EndX=0 EndY=10.5 EndZ=0
    g6: Circle [constr] CenterX=0 CenterY=0 CenterZ=0 NormalX=0 NormalY=0 NormalZ=1 AngleXU=0 Radius=10.5
    g7: LineSegment [constr] StartX=0 StartY=10.5 StartZ=0 EndX=0 EndY=-10.5 EndZ=0
    g8: Circle CenterX=0 CenterY=10.5 CenterZ=0 NormalX=0 NormalY=0 NormalZ=1 AngleXU=0 Radius=0.95
    g9: Circle CenterX=9.09327 CenterY=5.25 CenterZ=0 NormalX=0 NormalY=0 NormalZ=1 AngleXU=0 Radius=0.95
    g10: Circle CenterX=9.09327 CenterY=-5.25 CenterZ=0 NormalX=0 NormalY=0 NormalZ=1 AngleXU=0 Radius=0.95
    g11: Circle CenterX=0 CenterY=-10.5 CenterZ=0 NormalX=0 NormalY=0 NormalZ=1 AngleXU=0 Radius=0.95
    g12: Circle CenterX=-9.09327 CenterY=-5.25 CenterZ=0 NormalX=0 NormalY=0 NormalZ=1 AngleXU=0 Radius=0.95
    g13: Circle CenterX=-9.09327 CenterY=5.25 CenterZ=0 NormalX=0 NormalY=0 NormalZ=1 AngleXU=0 Radius=0.95
  constraints (30):
    c: Coincident(g0,g1)
    c: Coincident(g1,g2)
    c: Coincident(g2,g3)
    c: Coincident(g3,g4)
    c: Coincident(g4,g5)
    c: Coincident(g5,g0)
    c: Equal(g0, g1-g5) x5
    c: PointOnObject(g0,g6)
    c: PointOnObject(g1,g6)
    c: PointOnObject(g2,g6)
    c: PointOnObject(g3,g6)
    c: PointOnObject(g4,g6)
    c: PointOnObject(g5,g6)
    c: Coincident(g6,g-1)
    c: Coincident(g7,g0)
    c: Coincident(g7,g2)
    c: Radius(g6) = 10.5
    c: Coincident(g8,g0)
    c: Coincident(g9,g4)
    c: Coincident(g10,g3)
    c: Coincident(g11,g2)
    c: Coincident(g12,g1)
    c: Coincident(g13,g0)
    c: Equal(g13,g12)
    c: Equal(g12,g11)
    c: Equal(g11,g10)
    c: Equal(g10,g9)
    c: Equal(g9,g8)
    c: Radius(g8) = 0.95
    c: PointOnObject(g8,g-2)
FEATURE [PartDesign::Groove] Groove060  label="M3 Nut Smooth058"
  Angle = 360
  Axis = (-2e-16,3e-16,1)
  Base = (0,0,0)
  BaseFeature = -> Pad303
  Profile = -> Sketch724
  ReferenceAxis = -> Sketch724 [V_Axis]
  Reversed = true
FEATURE [PartDesign::Chamfer] Chamfer171  label="M3 Nut Smooth Hole070"
  Base = -> Groove060 [Edge24,Edge23]
  BaseFeature = -> Groove060
  Size = 0.2
FEATURE [PartDesign::Body] Body180  label="M2 Nut030"
  Group = -> [Sketch734,Pad303,Sketch724,Groove060,Chamfer171,Sketch728,Sketch716]
  Origin = -> Origin246
  Placement = pos=(0,0,2.75) rot=(0,0,1;0rad)
  Tip = -> Chamfer171
FEATURE [PartDesign::Pad] Pad305  label="Baseplate014"
  Length = 5
  Length2 = 100
  Profile = -> Sketch775
  Type = 0
FEATURE [Sketcher::SketchObject] Sketch774
  MapMode = 5
  Placement = pos=(-40,0,0) rot=(0.57735,-0.57735,-0.57735;2.0944rad)
  Support = -> [Pad305]
  sketch-geometry (4):
    g0: ArcOfCircle CenterX=-25 CenterY=-21 CenterZ=0 NormalX=0 NormalY=0 NormalZ=1 AngleXU=0 Radius=26 StartAngle=1.17601 EndAngle=1.5708
    g1: LineSegment StartX=-25 StartY=5 StartZ=0 EndX=-25 EndY=6 EndZ=0
    g2: LineSegment StartX=-25 StartY=6 StartZ=0 EndX=-15 EndY=6 EndZ=0
    g3: LineSegment StartX=-15 StartY=6 StartZ=0 EndX=-15 EndY=3 EndZ=0
  constraints (13):
    c: Coincident(g1,g0)
    c: Vertical(g1)
    c: Horizontal(g2)
    c: Coincident(g3,g2)
    c: Vertical(g3)
    c: Coincident(g0,g3)
    c: Coincident(g1,g2)
    c: DistanceY(g1,g1) = 1
    c: DistanceY(g3,g3) = 3
    c: DistanceX(g2,g2) = 10
    c: DistanceY(g-1,g0) = 5
    c: Perpendicular(g0,g1)
    c: DistanceX(g0,g-1) = 15
FEATURE [PartDesign::SubtractivePipe] SubtractivePipe006  label="Smooth Surfaces003"
  AuxilleryCurvelinear = true
  AuxillerySpineTangent = false
  BaseFeature = -> Pad305
  Binormal = (0,0,0)
  Mode = 0
  Profile = -> Sketch774
  Spine = -> Pad305 [Edge19,Edge22,Edge24,Edge4,Edge7,Edge10,Edge13]
  SpineTangent = false
  Transformation = 0
  Transition = 0
FEATURE [Sketcher::SketchObject] Sketch764
  MapMode = 5
  Placement = pos=(0,0,5) rot=(0,0,1;0rad)
  Support = -> [SubtractivePipe006]
  sketch-geometry (3):
    g0: Circle [constr] CenterX=0 CenterY=15 CenterZ=0 NormalX=0 NormalY=0 NormalZ=1 AngleXU=0 Radius=35
    g1: Circle CenterX=-33.541 CenterY=25 CenterZ=0 NormalX=0 NormalY=0 NormalZ=1 AngleXU=0 Radius=2.85
    g2: Circle CenterX=-28.7228 CenterY=35 CenterZ=0 NormalX=0 NormalY=0 NormalZ=1 AngleXU=0 Radius=2.85
  constraints (9):
    c: PointOnObject(g1,g0)
    c: PointOnObject(g2,g0)
    c: Radius(g0) = 35
    c: Equal(g2,g1)
    c: Radius(g1) = 2.85
    c: DistanceY(g1,g2) = 10
    c: DistanceY(g-1,g0) = 15
    c: DistanceY(g0,g1) = 10
    c: DistanceX(g0,g-1) = 0
FEATURE [PartDesign::Fillet] Fillet097  label="Smooth Edges007"
  Base = -> SubtractivePipe006 [Edge21]
  BaseFeature = -> SubtractivePipe006
  Radius = 1.5
FEATURE [PartDesign::Pocket] Pocket294  label="Servohorn Mounting Holes002"
  BaseFeature = -> Fillet088
  Length = 3
  Length2 = 100
  Profile = -> Sketch717
  Type = 0
FEATURE [Sketcher::SketchObject] Sketch726
  MapMode = 5
  Placement = pos=(0,0,3) rot=(0,0,1;0rad)
  Support = -> [Pocket294]
  sketch-geometry (1):
    g0: Circle CenterX=0 CenterY=0 CenterZ=0 NormalX=0 NormalY=0 NormalZ=1 AngleXU=0 Radius=6.15
  constraints (2):
    c: Coincident(g0,g-1)
    c: Radius(g0) = 6.15
FEATURE [PartDesign::Pocket] Pocket288  label="Servohorn Axis002"
  BaseFeature = -> Pocket294
  Length = 3
  Length2 = 100
  Profile = -> Sketch726
  Type = 0
FEATURE [PartDesign::Fillet] Fillet094  label="Smooth End Egde002"
  Base = -> Pocket288 [Edge150]
  BaseFeature = -> Pocket288
  Radius = 0.4
FEATURE [PartDesign::Body] Body185  label="Limb_Servohorn_Mount_long_v006"
  Group = -> [Sketch727,Pad304,Sketch712,SubtractivePipe007,Fillet096,Sketch722,Pocket293,Sketch721,Pocket283,Sketch718,Pocket287,Fillet088,Sketch717,Pocket294,Sketch726,Pocket288,Fillet094]
  Origin = -> Origin247
  Tip = -> Fillet094
FEATURE [PartDesign::Pad] Pad306  label="M3x8 Head037"
  Length = 2
  Length2 = 100
  Profile = -> Sketch730
  Type = 0
FEATURE [Sketcher::SketchObject] Sketch743
  MapMode = 5
  Placement = pos=(0,0,2) rot=(0,0,1;0rad)
  Support = -> [Pad306]
  sketch-geometry (1):
    g0: Circle CenterX=0 CenterY=0 CenterZ=0 NormalX=0 NormalY=0 NormalZ=1 AngleXU=0 Radius=1
  constraints (2):
    c: Coincident(g0,g-1)
    c: Radius(g0) = 1
FEATURE [PartDesign::Pad] Pad300  label="M3x8 Thread036"
  BaseFeature = -> Pad306
  Length = 8
  Length2 = 100
  Profile = -> Sketch743
  Type = 0
FEATURE [Sketcher::SketchObject] Sketch745
  MapMode = 5
  Placement = pos=(0,0,0) rot=(1,0,0;3.14159rad)
  Support = -> [Pad300]
  sketch-geometry (7):
    g0: LineSegment StartX=0.77 StartY=0.44456 StartZ=0 EndX=0 EndY=0.889119 EndZ=0
    g1: LineSegment StartX=0 StartY=0.889119 StartZ=0 EndX=-0.77 EndY=0.44456 EndZ=0
    g2: LineSegment StartX=-0.77 StartY=0.44456 StartZ=0 EndX=-0.77 EndY=-0.44456 EndZ=0
    g3: LineSegment StartX=-0.77 StartY=-0.44456 StartZ=0 EndX=3.85628e-11 EndY=-0.889119 EndZ=0
    g4: LineSegment StartX=3.85628e-11 StartY=-0.889119 StartZ=0 EndX=0.77 EndY=-0.44456 EndZ=0
    g5: LineSegment StartX=0.77 StartY=-0.44456 StartZ=0 EndX=0.77 EndY=0.44456 EndZ=0
    g6: Circle [constr] CenterX=0 CenterY=0 CenterZ=0 NormalX=0 NormalY=0 NormalZ=1 AngleXU=0 Radius=0.889119
  constraints (16):
    c: Coincident(g0,g1)
    c: Coincident(g1,g2)
    c: Coincident(g2,g3)
    c: Coincident(g3,g4)
    c: Coincident(g4,g5)
    c: Coincident(g5,g0)
    c: Equal(g0, g1-g5) x5
    c: PointOnObject(g0,g6)
    c: PointOnObject(g1,g6)
    c: PointOnObject(g2,g6)
    c: PointOnObject(g3,g6)
    c: PointOnObject(g4,g6)
    c: PointOnObject(g5,g6)
    c: Coincident(g6,g-1)
    c: PointOnObject(g0,g-2)
    c: DistanceX(g1,g0) = 1.54
FEATURE [PartDesign::Pocket] Pocket290  label="M3x8 Wrench036"
  BaseFeature = -> Pad300
  Length = 1
  Length2 = 100
  Profile = -> Sketch745
  Type = 0
FEATURE [PartDesign::Chamfer] Chamfer178  label="M3x8 Smooth053"
  Base = -> Pocket290 [Face11,Edge2,Edge24,Edge3]
  BaseFeature = -> Pocket290
  Size = 0.2
FEATURE [PartDesign::Body] Body186  label="M2x038"
  Group = -> [Sketch730,Pad306,Sketch743,Pad300,Sketch745,Pocket290,Chamfer178]
  Origin = -> Origin245
  Tip = -> Chamfer178
FEATURE [App::Part] Part094  label="M036"
  Group = -> [Body186,Body182]
  Origin = -> Origin253
  Placement = pos=(-9.8e-15,-10.5,80) rot=(0,1,0;3.14159rad)
FEATURE [PartDesign::Groove] Groove061  label="M3 Nut Smooth059"
  Angle = 360
  Axis = (-2e-16,3e-16,1)
  Base = (0,0,0)
  BaseFeature = -> Pad295
  Profile = -> Sketch731
  ReferenceAxis = -> Sketch731 [V_Axis]
  Reversed = true
FEATURE [PartDesign::Chamfer] Chamfer175  label="M3 Nut Smooth Hole072"
  Base = -> Groove061 [Edge24,Edge23]
  BaseFeature = -> Groove061
  Size = 0.2
FEATURE [PartDesign::Body] Body181  label="M2 Nut031"
  Group = -> [Sketch735,Pad295,Sketch731,Groove061,Chamfer175,Sketch740,Sketch739]
  Origin = -> Origin244
  Placement = pos=(0,0,2.75) rot=(0,0,1;0rad)
  Tip = -> Chamfer175
FEATURE [PartDesign::Pad] Pad307  label="M3x8 Thread038"
  BaseFeature = -> Pad294
  Length = 8
  Length2 = 100
  Profile = -> Sketch750
  Type = 0
FEATURE [Sketcher::SketchObject] Sketch741
  MapMode = 5
  Placement = pos=(0,0,0) rot=(1,0,0;3.14159rad)
  Support = -> [Pad307]
  sketch-geometry (7):
    g0: LineSegment StartX=0.77 StartY=0.44456 StartZ=0 EndX=0 EndY=0.889119 EndZ=0
    g1: LineSegment StartX=0 StartY=0.889119 StartZ=0 EndX=-0.77 EndY=0.44456 EndZ=0
    g2: LineSegment StartX=-0.77 StartY=0.44456 StartZ=0 EndX=-0.77 EndY=-0.44456 EndZ=0
    g3: LineSegment StartX=-0.77 StartY=-0.44456 StartZ=0 EndX=3.85628e-11 EndY=-0.889119 EndZ=0
    g4: LineSegment StartX=3.85628e-11 StartY=-0.889119 StartZ=0 EndX=0.77 EndY=-0.44456 EndZ=0
    g5: LineSegment StartX=0.77 StartY=-0.44456 StartZ=0 EndX=0.77 EndY=0.44456 EndZ=0
    g6: Circle [constr] CenterX=0 CenterY=0 CenterZ=0 NormalX=0 NormalY=0 NormalZ=1 AngleXU=0 Radius=0.889119
  constraints (16):
    c: Coincident(g0,g1)
    c: Coincident(g1,g2)
    c: Coincident(g2,g3)
    c: Coincident(g3,g4)
    c: Coincident(g4,g5)
    c: Coincident(g5,g0)
    c: Equal(g0, g1-g5) x5
    c: PointOnObject(g0,g6)
    c: PointOnObject(g1,g6)
    c: PointOnObject(g2,g6)
    c: PointOnObject(g3,g6)
    c: PointOnObject(g4,g6)
    c: PointOnObject(g5,g6)
    c: Coincident(g6,g-1)
    c: PointOnObject(g0,g-2)
    c: DistanceX(g1,g0) = 1.54
FEATURE [PartDesign::Pad] Pad308  label="M3 Nut Primitive059"
  Length = 0.6
  Length2 = 0.6
  Profile = -> Sketch736
  Type = 4
FEATURE [Sketcher::SketchObject] Sketch753
  ExternalGeometry = -> [Pad308]
  MapMode = 5
  Placement = pos=(0,0,0) rot=(0.57735,0.57735,0.57735;2.0944rad)
  Support = -> [YZ_Plane259]
  sketch-geometry (6):
    g0: LineSegment StartX=-1.9594 StartY=0.6 StartZ=0 EndX=-2.8094 EndY=0.6 EndZ=0
    g1: LineSegment StartX=-2.8094 StartY=0.6 StartZ=0 EndX=-2.8094 EndY=-0.6 EndZ=0
    g2: LineSegment StartX=-2.8094 StartY=-0.6 StartZ=0 EndX=-1.9594 EndY=-0.6 EndZ=0
    g3: LineSegment StartX=-1.9594 StartY=-0.6 StartZ=0 EndX=-2.3094 EndY=-0.4 EndZ=0
    g4: LineSegment StartX=-2.3094 StartY=-0.4 StartZ=0 EndX=-2.3094 EndY=0.4 EndZ=0
    g5: LineSegment StartX=-2.3094 StartY=0.4 StartZ=0 EndX=-1.9594 EndY=0.6 EndZ=0
  constraints (15):
    c: Horizontal(g0)
    c: Coincident(g0,g1)
    c: Coincident(g1,g2)
    c: Coincident(g2,g3)
    c: Coincident(g3,g4)
    c: Coincident(g4,g5)
    c: Coincident(g5,g0)
    c: Symmetric(g4,g3,g-1)
    c: Symmetric(g0,g2,g-1)
    c: Symmetric(g1,g0,g-1)
    c: DistanceX(g0,g4) = 0.5
    c: DistanceY(g3,g4) = 0.8
    c: DistanceY(g1,g0) = 1.2
    c: PointOnObject(g3,g-3)
    c: DistanceX(g4,g0) = 0.35
FEATURE [PartDesign::Groove] Groove058  label="M3 Nut Smooth056"
  Angle = 360
  Axis = (-2e-16,3e-16,1)
  Base = (0,0,0)
  BaseFeature = -> Pad308
  Profile = -> Sketch753
  ReferenceAxis = -> Sketch753 [V_Axis]
  Reversed = true
FEATURE [PartDesign::Chamfer] Chamfer176  label="M3 Nut Smooth Hole073"
  Base = -> Groove058 [Edge24,Edge23]
  BaseFeature = -> Groove058
  Size = 0.2
FEATURE [PartDesign::Body] Body173  label="M2 Nut028"
  Group = -> [Sketch736,Pad308,Sketch753,Groove058,Chamfer176,Sketch766,Sketch755]
  Origin = -> Origin254
  Placement = pos=(0,0,2.75) rot=(0,0,1;0rad)
  Tip = -> Chamfer176
FEATURE [App::Part] Part087  label="M032"
  Group = -> [Body174,Body173]
  Origin = -> Origin243
  Placement = pos=(9.1,-5.25,80) rot=(0,1,0;3.14159rad)
FEATURE [PartDesign::Pocket] Pocket296  label="M3x8 Wrench038"
  BaseFeature = -> Pad307
  Length = 1
  Length2 = 100
  Profile = -> Sketch741
  Type = 0
FEATURE [PartDesign::Chamfer] Chamfer174  label="M3x8 Smooth051"
  Base = -> Pocket296 [Face11,Edge2,Edge24,Edge3]
  BaseFeature = -> Pocket296
  Size = 0.2
FEATURE [PartDesign::Body] Body184  label="M2x037"
  Group = -> [Sketch729,Pad294,Sketch750,Pad307,Sketch741,Pocket296,Chamfer174]
  Origin = -> Origin242
  Tip = -> Chamfer174
FEATURE [App::Part] Part088  label="M033"
  Group = -> [Body184,Body181]
  Origin = -> Origin239
  Placement = pos=(-9.1,-5.25,80) rot=(0,1,0;3.14159rad)
FEATURE [PartDesign::Pad] Pad310  label="M3x8 Head038"
  Length = 2
  Length2 = 100
  Profile = -> Sketch723
  Type = 0
FEATURE [Sketcher::SketchObject] Sketch725
  MapMode = 5
  Placement = pos=(0,0,2) rot=(0,0,1;0rad)
  Support = -> [Pad310]
  sketch-geometry (1):
    g0: Circle CenterX=0 CenterY=0 CenterZ=0 NormalX=0 NormalY=0 NormalZ=1 AngleXU=0 Radius=1
  constraints (2):
    c: Coincident(g0,g-1)
    c: Radius(g0) = 1
FEATURE [PartDesign::Pad] Pad302  label="M3x8 Thread037"
  BaseFeature = -> Pad310
  Length = 8
  Length2 = 100
  Profile = -> Sketch725
  Type = 0
FEATURE [Sketcher::SketchObject] Sketch738
  MapMode = 5
  Placement = pos=(0,0,0) rot=(1,0,0;3.14159rad)
  Support = -> [Pad302]
  sketch-geometry (7):
    g0: LineSegment StartX=0.77 StartY=0.44456 StartZ=0 EndX=0 EndY=0.889119 EndZ=0
    g1: LineSegment StartX=0 StartY=0.889119 StartZ=0 EndX=-0.77 EndY=0.44456 EndZ=0
    g2: LineSegment StartX=-0.77 StartY=0.44456 StartZ=0 EndX=-0.77 EndY=-0.44456 EndZ=0
    g3: LineSegment StartX=-0.77 StartY=-0.44456 StartZ=0 EndX=3.85628e-11 EndY=-0.889119 EndZ=0
    g4: LineSegment StartX=3.85628e-11 StartY=-0.889119 StartZ=0 EndX=0.77 EndY=-0.44456 EndZ=0
    g5: LineSegment StartX=0.77 StartY=-0.44456 StartZ=0 EndX=0.77 EndY=0.44456 EndZ=0
    g6: Circle [constr] CenterX=0 CenterY=0 CenterZ=0 NormalX=0 NormalY=0 NormalZ=1 AngleXU=0 Radius=0.889119
  constraints (16):
    c: Coincident(g0,g1)
    c: Coincident(g1,g2)
    c: Coincident(g2,g3)
    c: Coincident(g3,g4)
    c: Coincident(g4,g5)
    c: Coincident(g5,g0)
    c: Equal(g0, g1-g5) x5
    c: PointOnObject(g0,g6)
    c: PointOnObject(g1,g6)
    c: PointOnObject(g2,g6)
    c: PointOnObject(g3,g6)
    c: PointOnObject(g4,g6)
    c: PointOnObject(g5,g6)
    c: Coincident(g6,g-1)
    c: PointOnObject(g0,g-2)
    c: DistanceX(g1,g0) = 1.54
FEATURE [PartDesign::Pocket] Pocket295  label="M3x8 Wrench037"
  BaseFeature = -> Pad302
  Length = 1
  Length2 = 100
  Profile = -> Sketch738
  Type = 0
FEATURE [PartDesign::Chamfer] Chamfer172  label="M3x8 Smooth050"
  Base = -> Pocket295 [Face11,Edge2,Edge24,Edge3]
  BaseFeature = -> Pocket295
  Size = 0.2
FEATURE [PartDesign::Body] Body183  label="M2x036"
  Group = -> [Sketch723,Pad310,Sketch725,Pad302,Sketch738,Pocket295,Chamfer172]
  Origin = -> Origin241
  Tip = -> Chamfer172
FEATURE [App::Part] Part089  label="M034"
  Group = -> [Body183,Body180]
  Origin = -> Origin237
  Placement = pos=(-9.8e-15,10.5,80) rot=(0,1,0;3.14159rad)
FEATURE [PartDesign::Pad] Pad313  label="M3x8 Head039"
  Length = 2
  Length2 = 100
  Profile = -> Sketch749
  Type = 0
FEATURE [Sketcher::SketchObject] Sketch754
  MapMode = 5
  Placement = pos=(0,0,2) rot=(0,0,1;0rad)
  Support = -> [Pad313]
  sketch-geometry (1):
    g0: Circle CenterX=0 CenterY=0 CenterZ=0 NormalX=0 NormalY=0 NormalZ=1 AngleXU=0 Radius=1
  constraints (2):
    c: Coincident(g0,g-1)
    c: Radius(g0) = 1
FEATURE [PartDesign::Pad] Pad314  label="M3 Nut Primitive060"
  Length = 0.6
  Length2 = 0.6
  Profile = -> Sketch751
  Type = 4
FEATURE [Sketcher::SketchObject] Sketch742
  ExternalGeometry = -> [Pad314]
  MapMode = 5
  Placement = pos=(0,0,0) rot=(0.57735,0.57735,0.57735;2.0944rad)
  Support = -> [YZ_Plane250]
  sketch-geometry (6):
    g0: LineSegment StartX=-1.9594 StartY=0.6 StartZ=0 EndX=-2.8094 EndY=0.6 EndZ=0
    g1: LineSegment StartX=-2.8094 StartY=0.6 StartZ=0 EndX=-2.8094 EndY=-0.6 EndZ=0
    g2: LineSegment StartX=-2.8094 StartY=-0.6 StartZ=0 EndX=-1.9594 EndY=-0.6 EndZ=0
    g3: LineSegment StartX=-1.9594 StartY=-0.6 StartZ=0 EndX=-2.3094 EndY=-0.4 EndZ=0
    g4: LineSegment StartX=-2.3094 StartY=-0.4 StartZ=0 EndX=-2.3094 EndY=0.4 EndZ=0
    g5: LineSegment StartX=-2.3094 StartY=0.4 StartZ=0 EndX=-1.9594 EndY=0.6 EndZ=0
  constraints (15):
    c: Horizontal(g0)
    c: Coincident(g0,g1)
    c: Coincident(g1,g2)
    c: Coincident(g2,g3)
    c: Coincident(g3,g4)
    c: Coincident(g4,g5)
    c: Coincident(g5,g0)
    c: Symmetric(g4,g3,g-1)
    c: Symmetric(g0,g2,g-1)
    c: Symmetric(g1,g0,g-1)
    c: DistanceX(g0,g4) = 0.5
    c: DistanceY(g3,g4) = 0.8
    c: DistanceY(g1,g0) = 1.2
    c: PointOnObject(g3,g-3)
    c: DistanceX(g4,g0) = 0.35
FEATURE [PartDesign::Groove] Groove062  label="M3 Nut Smooth060"
  Angle = 360
  Axis = (-2e-16,3e-16,1)
  Base = (0,0,0)
  BaseFeature = -> Pad314
  Profile = -> Sketch742
  ReferenceAxis = -> Sketch742 [V_Axis]
  Reversed = true
FEATURE [PartDesign::Chamfer] Chamfer131  label="M3 Nut Smooth Hole056"
  Base = -> Groove062 [Edge24,Edge23]
  BaseFeature = -> Groove062
  Size = 0.2
FEATURE [PartDesign::Body] Body172  label="M2 Nut027"
  Group = -> [Sketch751,Pad314,Sketch742,Groove062,Chamfer131,Sketch756,Sketch759]
  Origin = -> Origin255
  Placement = pos=(0,0,2.75) rot=(0,0,1;0rad)
  Tip = -> Chamfer131
FEATURE [PartDesign::Pad] Pad319  label="M3x8 Head041"
  Length = 2
  Length2 = 100
  Profile = -> Sketch770
  Type = 0
FEATURE [Sketcher::SketchObject] Sketch760
  MapMode = 5
  Placement = pos=(0,0,2) rot=(0,0,1;0rad)
  Support = -> [Pad319]
  sketch-geometry (1):
    g0: Circle CenterX=0 CenterY=0 CenterZ=0 NormalX=0 NormalY=0 NormalZ=1 AngleXU=0 Radius=1
  constraints (2):
    c: Coincident(g0,g-1)
    c: Radius(g0) = 1
FEATURE [PartDesign::Pad] Pad309  label="M3x8 Thread039"
  BaseFeature = -> Pad319
  Length = 8
  Length2 = 100
  Profile = -> Sketch760
  Type = 0
FEATURE [Sketcher::SketchObject] Sketch744
  MapMode = 5
  Placement = pos=(0,0,0) rot=(1,0,0;3.14159rad)
  Support = -> [Pad309]
  sketch-geometry (7):
    g0: LineSegment StartX=0.77 StartY=0.44456 StartZ=0 EndX=0 EndY=0.889119 EndZ=0
    g1: LineSegment StartX=0 StartY=0.889119 StartZ=0 EndX=-0.77 EndY=0.44456 EndZ=0
    g2: LineSegment StartX=-0.77 StartY=0.44456 StartZ=0 EndX=-0.77 EndY=-0.44456 EndZ=0
    g3: LineSegment StartX=-0.77 StartY=-0.44456 StartZ=0 EndX=3.85628e-11 EndY=-0.889119 EndZ=0
    g4: LineSegment StartX=3.85628e-11 StartY=-0.889119 StartZ=0 EndX=0.77 EndY=-0.44456 EndZ=0
    g5: LineSegment StartX=0.77 StartY=-0.44456 StartZ=0 EndX=0.77 EndY=0.44456 EndZ=0
    g6: Circle [constr] CenterX=0 CenterY=0 CenterZ=0 NormalX=0 NormalY=0 NormalZ=1 AngleXU=0 Radius=0.889119
  constraints (16):
    c: Coincident(g0,g1)
    c: Coincident(g1,g2)
    c: Coincident(g2,g3)
    c: Coincident(g3,g4)
    c: Coincident(g4,g5)
    c: Coincident(g5,g0)
    c: Equal(g0, g1-g5) x5
    c: PointOnObject(g0,g6)
    c: PointOnObject(g1,g6)
    c: PointOnObject(g2,g6)
    c: PointOnObject(g3,g6)
    c: PointOnObject(g4,g6)
    c: PointOnObject(g5,g6)
    c: Coincident(g6,g-1)
    c: PointOnObject(g0,g-2)
    c: DistanceX(g1,g0) = 1.54
FEATURE [PartDesign::Pocket] Pocket299  label="M3x8 Wrench039"
  BaseFeature = -> Pad309
  Length = 1
  Length2 = 100
  Profile = -> Sketch744
  Type = 0
FEATURE [PartDesign::Chamfer] Chamfer134  label="M3x8 Smooth037"
  Base = -> Pocket299 [Face11,Edge2,Edge24,Edge3]
  BaseFeature = -> Pocket299
  Size = 0.2
FEATURE [PartDesign::Body] Body179  label="M2x035"
  Group = -> [Sketch770,Pad319,Sketch760,Pad309,Sketch744,Pocket299,Chamfer134]
  Origin = -> Origin337
  Tip = -> Chamfer134
FEATURE [PartDesign::Pad] Pad320  label="M3x8 Thread040"
  BaseFeature = -> Pad313
  Length = 8
  Length2 = 100
  Profile = -> Sketch754
  Type = 0
FEATURE [Sketcher::SketchObject] Sketch758
  MapMode = 5
  Placement = pos=(0,0,0) rot=(1,0,0;3.14159rad)
  Support = -> [Pad320]
  sketch-geometry (7):
    g0: LineSegment StartX=0.77 StartY=0.44456 StartZ=0 EndX=0 EndY=0.889119 EndZ=0
    g1: LineSegment StartX=0 StartY=0.889119 StartZ=0 EndX=-0.77 EndY=0.44456 EndZ=0
    g2: LineSegment StartX=-0.77 StartY=0.44456 StartZ=0 EndX=-0.77 EndY=-0.44456 EndZ=0
    g3: LineSegment StartX=-0.77 StartY=-0.44456 StartZ=0 EndX=3.85628e-11 EndY=-0.889119 EndZ=0
    g4: LineSegment StartX=3.85628e-11 StartY=-0.889119 StartZ=0 EndX=0.77 EndY=-0.44456 EndZ=0
    g5: LineSegment StartX=0.77 StartY=-0.44456 StartZ=0 EndX=0.77 EndY=0.44456 EndZ=0
    g6: Circle [constr] CenterX=0 CenterY=0 CenterZ=0 NormalX=0 NormalY=0 NormalZ=1 AngleXU=0 Radius=0.889119
  constraints (16):
    c: Coincident(g0,g1)
    c: Coincident(g1,g2)
    c: Coincident(g2,g3)
    c: Coincident(g3,g4)
    c: Coincident(g4,g5)
    c: Coincident(g5,g0)
    c: Equal(g0, g1-g5) x5
    c: PointOnObject(g0,g6)
    c: PointOnObject(g1,g6)
    c: PointOnObject(g2,g6)
    c: PointOnObject(g3,g6)
    c: PointOnObject(g4,g6)
    c: PointOnObject(g5,g6)
    c: Coincident(g6,g-1)
    c: PointOnObject(g0,g-2)
    c: DistanceX(g1,g0) = 1.54
FEATURE [PartDesign::Pocket] Pocket305  label="M3x8 Wrench040"
  BaseFeature = -> Pad320
  Length = 1
  Length2 = 100
  Profile = -> Sketch758
  Type = 0
FEATURE [PartDesign::Chamfer] Chamfer133  label="M3x8 Smooth036"
  Base = -> Pocket305 [Face11,Edge2,Edge24,Edge3]
  BaseFeature = -> Pocket305
  Size = 0.2
FEATURE [PartDesign::Pocket] Pocket311  label="Screwheads Montage004"
  BaseFeature = -> Fillet097
  Length = 3
  Length2 = 100
  Profile = -> Sketch764
  Type = 0
FEATURE [Sketcher::SketchObject] Sketch765
  MapMode = 5
  Placement = pos=(0,0,2) rot=(0,0,1;0rad)
  Support = -> [Pocket311]
  sketch-geometry (3):
    g0: Circle [constr] CenterX=0 CenterY=15 CenterZ=0 NormalX=0 NormalY=0 NormalZ=1 AngleXU=0 Radius=35
    g1: Circle CenterX=-33.541 CenterY=25 CenterZ=0 NormalX=0 NormalY=0 NormalZ=1 AngleXU=0 Radius=1.6
    g2: Circle CenterX=-28.7228 CenterY=35 CenterZ=0 NormalX=0 NormalY=0 NormalZ=1 AngleXU=0 Radius=1.6
  constraints (9):
    c: Radius(g0) = 35
    c: PointOnObject(g1,g0)
    c: PointOnObject(g2,g0)
    c: Equal(g2,g1)
    c: Radius(g2) = 1.6
    c: DistanceY(g1,g2) = 10
    c: DistanceY(g-1,g0) = 15
    c: DistanceY(g0,g1) = 10
    c: DistanceX(g0,g-1) = 0
FEATURE [PartDesign::Pocket] Pocket312  label="Screwholes Montage004"
  BaseFeature = -> Pocket311
  Length = 3
  Length2 = 100
  Profile = -> Sketch765
  Type = 0
FEATURE [Sketcher::SketchObject] Sketch769
  MapMode = 5
  Placement = pos=(0,0,5) rot=(0,0,1;0rad)
  Support = -> [Pocket312]
  sketch-geometry (1):
    g0: Circle CenterX=0 CenterY=0 CenterZ=0 NormalX=0 NormalY=0 NormalZ=1 AngleXU=0 Radius=6.15
  constraints (2):
    c: Coincident(g0,g-1)
    c: Radius(g0) = 6.15
FEATURE [PartDesign::Pocket] Pocket300  label="Ball Bearing Flange001"
  BaseFeature = -> Pocket312
  Length = 5
  Length2 = 100
  Profile = -> Sketch769
  Type = 0
FEATURE [Sketcher::SketchObject] Sketch771
  MapMode = 5
  Placement = pos=(0,0,0) rot=(1,0,0;3.14159rad)
  Support = -> [Pocket300]
  sketch-geometry (1):
    g0: Circle CenterX=0 CenterY=0 CenterZ=0 NormalX=0 NormalY=0 NormalZ=1 AngleXU=0 Radius=8.15
  constraints (2):
    c: Coincident(g0,g-1)
    c: Radius(g0) = 8.15
FEATURE [PartDesign::Pocket] Pocket298  label="Ball Bearing Pocket001"
  BaseFeature = -> Pocket300
  Length = 4.5
  Length2 = 100
  Profile = -> Sketch771
  Type = 0
FEATURE [PartDesign::Fillet] Fillet095  label="Ball Bearing Pocket Bottom Fillet001"
  Base = -> Pocket298 [Edge43]
  BaseFeature = -> Pocket298
  Radius = 1.8
FEATURE [PartDesign::Fillet] Fillet098  label="Smooth End Edge001"
  Base = -> Fillet095 [Edge31]
  BaseFeature = -> Fillet095
  Radius = 0.4
FEATURE [PartDesign::Body] Body169  label="Limb_Ball_Bearing_Mount_long_v005"
  Group = -> [Sketch775,Pad305,Sketch774,SubtractivePipe006,Fillet097,Sketch764,Pocket311,Sketch765,Pocket312,Sketch769,Pocket300,Sketch771,Pocket298,Fillet095,Fillet098]
  Origin = -> Origin349
  Tip = -> Fillet098
FEATURE [App::Part] Part092  label="ball bearing moung001"
  Group = -> [Body169]
  Origin = -> Origin335
  Placement = pos=(-144.1,22.7,27.05) rot=(0,0.707107,0.707107;3.14159rad)
FEATURE [PartDesign::Pad] Pad321  label="M3 Nut Primitive062"
  Length = 0.6
  Length2 = 0.6
  Profile = -> Sketch757
  Type = 4
FEATURE [Sketcher::SketchObject] Sketch767
  ExternalGeometry = -> [Pad321]
  MapMode = 5
  Placement = pos=(0,0,0) rot=(0.57735,0.57735,0.57735;2.0944rad)
  Support = -> [YZ_Plane246]
  sketch-geometry (6):
    g0: LineSegment StartX=-1.9594 StartY=0.6 StartZ=0 EndX=-2.8094 EndY=0.6 EndZ=0
    g1: LineSegment StartX=-2.8094 StartY=0.6 StartZ=0 EndX=-2.8094 EndY=-0.6 EndZ=0
    g2: LineSegment StartX=-2.8094 StartY=-0.6 StartZ=0 EndX=-1.9594 EndY=-0.6 EndZ=0
    g3: LineSegment StartX=-1.9594 StartY=-0.6 StartZ=0 EndX=-2.3094 EndY=-0.4 EndZ=0
    g4: LineSegment StartX=-2.3094 StartY=-0.4 StartZ=0 EndX=-2.3094 EndY=0.4 EndZ=0
    g5: LineSegment StartX=-2.3094 StartY=0.4 StartZ=0 EndX=-1.9594 EndY=0.6 EndZ=0
  constraints (15):
    c: Horizontal(g0)
    c: Coincident(g0,g1)
    c: Coincident(g1,g2)
    c: Coincident(g2,g3)
    c: Coincident(g3,g4)
    c: Coincident(g4,g5)
    c: Coincident(g5,g0)
    c: Symmetric(g4,g3,g-1)
    c: Symmetric(g0,g2,g-1)
    c: Symmetric(g1,g0,g-1)
    c: DistanceX(g0,g4) = 0.5
    c: DistanceY(g3,g4) = 0.8
    c: DistanceY(g1,g0) = 1.2
    c: PointOnObject(g3,g-3)
    c: DistanceX(g4,g0) = 0.35
FEATURE [PartDesign::Groove] Groove066  label="M3 Nut Smooth063"
  Angle = 360
  Axis = (-2e-16,3e-16,1)
  Base = (0,0,0)
  BaseFeature = -> Pad321
  Profile = -> Sketch767
  ReferenceAxis = -> Sketch767 [V_Axis]
  Reversed = true
FEATURE [PartDesign::Chamfer] Chamfer135  label="M3 Nut Smooth Hole057"
  Base = -> Groove066 [Edge24,Edge23]
  BaseFeature = -> Groove066
  Size = 0.2
FEATURE [PartDesign::Body] Body178  label="M2 Nut029"
  Group = -> [Sketch757,Pad321,Sketch767,Groove066,Chamfer135,Sketch772,Sketch768]
  Origin = -> Origin333
  Placement = pos=(0,0,2.75) rot=(0,0,1;0rad)
  Tip = -> Chamfer135
FEATURE [App::Part] Part083  label="M031"
  Group = -> [Body179,Body178]
  Origin = -> Origin334
  Placement = pos=(-9.1,5.25,80) rot=(0,1,0;3.14159rad)
FEATURE [PartDesign::Pad] Pad333  label="M3x20 Head024"
  Length = 3
  Length2 = 100
  Profile = -> Sketch792
  Type = 0
FEATURE [PartDesign::Pad] Pad334  label="M3x20 Head025"
  Length = 3
  Length2 = 100
  Profile = -> Sketch794
  Type = 0
FEATURE [PartDesign::Pad] Pad337  label="M3 Nut Primitive068"
  Length = 1.2
  Length2 = 1.2
  Profile = -> Sketch793
  Type = 4
FEATURE [PartDesign::Pad] Pad344  label="M3x20 Head026"
  Length = 3
  Length2 = 100
  Profile = -> Sketch782
  Type = 0
FEATURE [Sketcher::SketchObject] Sketch780
  MapMode = 5
  Placement = pos=(0,0,3) rot=(0,0,1;0rad)
  Support = -> [Pad344]
  sketch-geometry (1):
    g0: Circle CenterX=0 CenterY=0 CenterZ=0 NormalX=0 NormalY=0 NormalZ=1 AngleXU=0 Radius=1.5
  constraints (2):
    c: Coincident(g0,g-1)
    c: Radius(g0) = 1.5
FEATURE [PartDesign::Pad] Pad345
  Length = 10
  Length2 = 100
  Placement = pos=(0,0,0) rot=(1,0,0;1.5708rad)
  Profile = -> Sketch783
  Reversed = true
  Type = 0
FEATURE [PartDesign::Pad] Pad346  label="M3x20 Thread027"
  BaseFeature = -> Pad344
  Length = 20
  Length2 = 100
  Profile = -> Sketch780
  Type = 0
FEATURE [Sketcher::SketchObject] Sketch786
  MapMode = 5
  Placement = pos=(0,0,0) rot=(1,0,0;3.14159rad)
  Support = -> [Pad346]
  sketch-geometry (7):
    g0: LineSegment StartX=1.275 StartY=0.736122 StartZ=0 EndX=0 EndY=1.47224 EndZ=0
    g1: LineSegment StartX=0 StartY=1.47224 StartZ=0 EndX=-1.275 EndY=0.736122 EndZ=0
    g2: LineSegment StartX=-1.275 StartY=0.736122 StartZ=0 EndX=-1.275 EndY=-0.736122 EndZ=0
    g3: LineSegment StartX=-1.275 StartY=-0.736122 StartZ=0 EndX=1.34766e-11 EndY=-1.47224 EndZ=0
    g4: LineSegment StartX=1.34766e-11 StartY=-1.47224 StartZ=0 EndX=1.275 EndY=-0.736122 EndZ=0
    g5: LineSegment StartX=1.275 StartY=-0.736122 StartZ=0 EndX=1.275 EndY=0.736122 EndZ=0
    g6: Circle [constr] CenterX=0 CenterY=0 CenterZ=0 NormalX=0 NormalY=0 NormalZ=1 AngleXU=0 Radius=1.47224
  constraints (16):
    c: Coincident(g0,g1)
    c: Coincident(g1,g2)
    c: Coincident(g2,g3)
    c: Coincident(g3,g4)
    c: Coincident(g4,g5)
    c: Coincident(g5,g0)
    c: Equal(g0, g1-g5) x5
    c: PointOnObject(g0,g6)
    c: PointOnObject(g1,g6)
    c: PointOnObject(g2,g6)
    c: PointOnObject(g3,g6)
    c: PointOnObject(g4,g6)
    c: PointOnObject(g5,g6)
    c: Coincident(g6,g-1)
    c: PointOnObject(g0,g-2)
    c: DistanceX(g1,g0) = 2.55
FEATURE [PartDesign::Pocket] Pocket323  label="M3x20 Wrench026"
  BaseFeature = -> Pad346
  Length = 1.3
  Length2 = 100
  Profile = -> Sketch786
  Type = 0
FEATURE [PartDesign::Chamfer] Chamfer180  label="M3x20 Smooth031"
  Base = -> Pocket323 [Face11,Edge2,Edge24,Edge3]
  BaseFeature = -> Pocket323
  Size = 0.2
FEATURE [PartDesign::Pad] Pad349
  Length = 5
  Length2 = 100
  Profile = -> Sketch790
  Type = 0
FEATURE [Sketcher::SketchObject] Sketch788
  ExternalGeometry = -> [Pad349]
  MapMode = 5
  Placement = pos=(0,0,5) rot=(0,0,1;0rad)
  Support = -> [Pad349]
  sketch-geometry (1):
    g0: Circle CenterX=0 CenterY=10.15 CenterZ=0 NormalX=0 NormalY=0 NormalZ=1 AngleXU=0 Radius=1.5
  constraints (2):
    c: Coincident(g0,g-3)
    c: Radius(g0) = 1.5
FEATURE [PartDesign::Pocket] Pocket332
  BaseFeature = -> Pad349
  Length = 4
  Length2 = 100
  Profile = -> Sketch788
  Type = 0
FEATURE [PartDesign::Fillet] Fillet101
  Base = -> Pad301 [Face5,Edge96,Face4]
  BaseFeature = -> Pad301
  Radius = 0.2
FEATURE [PartDesign::Body] Body175  label="Futuba FSH6B004"
  Group = -> [Sketch719,Pad298,Sketch714,Pocket289,Sketch720,Pocket284,Sketch713,Pocket286,Sketch715,Pad301,Fillet101]
  Origin = -> Origin317
  Tip = -> Fillet101
FEATURE [App::Part] Part091  label="Servohorn008"
  Group = -> [Body175]
  Origin = -> Origin248
  Placement = pos=(0,0,3) rot=(0,0,1;0rad)
FEATURE [PartDesign::Body] Body203
  Origin = -> Origin362
FEATURE [PartDesign::Body] Body222  label="M2x040"
  Group = -> [Sketch749,Pad313,Sketch754,Pad320,Sketch758,Pocket305,Chamfer133]
  Origin = -> Origin252
  Tip = -> Chamfer133
FEATURE [App::Part] Part093  label="M035"
  Group = -> [Body222,Body172]
  Origin = -> Origin251
  Placement = pos=(9.1,5.25,80) rot=(0,1,0;3.14159rad)
FEATURE [App::Part] Part086  label="Screws006"
  Group = -> [Part089,Part094,Part088,Part087,Part093,Part083]
  Origin = -> Origin238
  Placement = pos=(0,0,-71) rot=(0,0,1;0rad)
FEATURE [App::Part] Part082  label="servohorn moun tpost001"
  Group = -> [Body185,Part091,Part086]
  Origin = -> Origin240
  Placement = pos=(-144.1,-24.45,27.05) rot=(1,0,0;1.5708rad)
FEATURE [PartDesign::Body] Body225  label="orange wire007"
  Group = -> [Sketch783,Pad345]
  Origin = -> Origin331
  Placement = pos=(0,25.15,0) rot=(0,0,1;0rad)
  Tip = -> Pad345
FEATURE [PartDesign::Body] Body227  label="M3x053"
  Group = -> [Sketch782,Pad344,Sketch780,Pad346,Sketch786,Pocket323,Chamfer180]
  Origin = -> Origin364
  Placement = pos=(-114.75,-30,41) rot=(-1,0,0;1.5708rad)
  Tip = -> Chamfer180
FEATURE [PartDesign::Chamfer] Chamfer195
  Base = -> Pocket332 [Edge3]
  BaseFeature = -> Pocket332
  Size = 0.25
FEATURE [PartDesign::Body] Body189  label="Gear006"
  Group = -> [Sketch790,Pad349,Sketch788,Pocket332,Chamfer195]
  Origin = -> Origin370
  Placement = pos=(0,0,38.25) rot=(0,0,1;0rad)
  Tip = -> Chamfer195
FEATURE [Sketcher::SketchObject] Sketch795
  MapMode = 5
  Placement = pos=(0,0,0) rot=(1,0,0;1.5708rad)
  Support = -> [XZ_Plane266]
  sketch-geometry (1):
    g0: Circle CenterX=1.55 CenterY=4 CenterZ=0 NormalX=0 NormalY=0 NormalZ=1 AngleXU=0 Radius=0.75
  constraints (3):
    c: Radius(g0) = 0.75
    c: DistanceY(g-1,g0) = 4
    c: DistanceX(g-1,g0) = 1.55
FEATURE [PartDesign::Pad] Pad359
  Length = 10
  Length2 = 100
  Placement = pos=(0,0,0) rot=(1,0,0;1.5708rad)
  Profile = -> Sketch795
  Reversed = true
  Type = 0
FEATURE [PartDesign::Body] Body212  label="brown wire007"
  Group = -> [Sketch795,Pad359]
  Origin = -> Origin322
  Placement = pos=(0,25.15,0) rot=(0,0,1;0rad)
  Tip = -> Pad359
FEATURE [Sketcher::SketchObject] Sketch796
  MapMode = 5
  Placement = pos=(0,0,3) rot=(0,0,1;0rad)
  Support = -> [Pad333]
  sketch-geometry (1):
    g0: Circle CenterX=0 CenterY=0 CenterZ=0 NormalX=0 NormalY=0 NormalZ=1 AngleXU=0 Radius=1.5
  constraints (2):
    c: Coincident(g0,g-1)
    c: Radius(g0) = 1.5
FEATURE [PartDesign::Pad] Pad335  label="M3x20 Thread025"
  BaseFeature = -> Pad333
  Length = 20
  Length2 = 100
  Profile = -> Sketch796
  Type = 0
FEATURE [Sketcher::SketchObject] Sketch798
  MapMode = 5
  Placement = pos=(0,0,0) rot=(1,0,0;1.5708rad)
  Support = -> [XZ_Plane269]
  sketch-geometry (1):
    g0: Circle CenterX=0 CenterY=4 CenterZ=0 NormalX=0 NormalY=0 NormalZ=1 AngleXU=0 Radius=0.75
  constraints (3):
    c: PointOnObject(g0,g-2)
    c: Radius(g0) = 0.75
    c: DistanceY(g-1,g0) = 4
FEATURE [PartDesign::Pad] Pad350
  Length = 10
  Length2 = 100
  Placement = pos=(0,0,0) rot=(1,0,0;1.5708rad)
  Profile = -> Sketch798
  Reversed = true
  Type = 0
FEATURE [PartDesign::Body] Body176  label="red wire006"
  Group = -> [Sketch798,Pad350]
  Origin = -> Origin376
  Placement = pos=(0,25.15,0) rot=(0,0,1;0rad)
  Tip = -> Pad350
FEATURE [Sketcher::SketchObject] Sketch802
  MapMode = 5
  Support = -> [XY_Plane275]
  sketch-geometry (4):
    g0: LineSegment StartX=-10 StartY=20.15 StartZ=0 EndX=10 EndY=20.15 EndZ=0
    g1: LineSegment StartX=10 StartY=20.15 StartZ=0 EndX=10 EndY=-20.15 EndZ=0
    g2: LineSegment StartX=10 StartY=-20.15 StartZ=0 EndX=-10 EndY=-20.15 EndZ=0
    g3: LineSegment StartX=-10 StartY=-20.15 StartZ=0 EndX=-10 EndY=20.15 EndZ=0
  constraints (10):
    c: Coincident(g0,g1)
    c: Coincident(g1,g2)
    c: Coincident(g2,g3)
    c: Coincident(g3,g0)
    c: Horizontal(g2)
    c: Vertical(g3)
    c: DistanceX(g0,g0) = 20
    c: DistanceY(g1,g1) = 40.3
    c: Symmetric(g0,g1,g-1)
    c: Symmetric(g0,g0,g-2)
FEATURE [PartDesign::Pad] Pad326  label="Baseblock007"
  Length = 26.6
  Length2 = 100
  Profile = -> Sketch802
  Type = 0
FEATURE [Sketcher::SketchObject] Sketch779
  MapMode = 5
  Placement = pos=(0,0,26.6) rot=(0,0,1;0rad)
  Support = -> [Pad326]
  sketch-geometry (4):
    g0: LineSegment StartX=-10 StartY=-26.8 StartZ=0 EndX=10 EndY=-26.8 EndZ=0
    g1: LineSegment StartX=10 StartY=-26.8 StartZ=0 EndX=10 EndY=26.8 EndZ=0
    g2: LineSegment StartX=10 StartY=26.8 StartZ=0 EndX=-10 EndY=26.8 EndZ=0
    g3: LineSegment StartX=-10 StartY=26.8 StartZ=0 EndX=-10 EndY=-26.8 EndZ=0
  constraints (10):
    c: Coincident(g0,g1)
    c: Coincident(g1,g2)
    c: Coincident(g2,g3)
    c: Coincident(g3,g0)
    c: Horizontal(g0)
    c: Vertical(g3)
    c: Symmetric(g1,g2,g-2)
    c: Symmetric(g1,g0,g-1)
    c: DistanceX(g2,g2) = 20
    c: DistanceY(g1,g1) = 53.6
FEATURE [PartDesign::Pad] Pad356
  BaseFeature = -> Pad326
  Length = 2.5
  Length2 = 100
  Profile = -> Sketch779
  Type = 0
FEATURE [Sketcher::SketchObject] Sketch784
  MapMode = 5
  Placement = pos=(0,0,29.1) rot=(0,0,1;0rad)
  Support = -> [Pad356]
  sketch-geometry (4):
    g0: LineSegment StartX=-10 StartY=-20.15 StartZ=0 EndX=10 EndY=-20.15 EndZ=0
    g1: LineSegment StartX=10 StartY=-20.15 StartZ=0 EndX=10 EndY=20.15 EndZ=0
    g2: LineSegment StartX=10 StartY=20.15 StartZ=0 EndX=-10 EndY=20.15 EndZ=0
    g3: LineSegment StartX=-10 StartY=20.15 StartZ=0 EndX=-10 EndY=-20.15 EndZ=0
  constraints (10):
    c: Coincident(g0,g1)
    c: Coincident(g1,g2)
    c: Coincident(g2,g3)
    c: Coincident(g3,g0)
    c: Horizontal(g0)
    c: Vertical(g3)
    c: Symmetric(g1,g2,g-2)
    c: Symmetric(g1,g0,g-1)
    c: DistanceX(g2,g2) = 20
    c: DistanceY(g1,g1) = 40.3
FEATURE [PartDesign::Pad] Pad351
  BaseFeature = -> Pad356
  Length = 6
  Length2 = 100
  Profile = -> Sketch784
  Type = 0
FEATURE [Sketcher::SketchObject] Sketch787
  ExternalGeometry = -> [Pad351]
  MapMode = 5
  Placement = pos=(0,0,35.1) rot=(0,0,1;0rad)
  Support = -> [Pad351]
  sketch-geometry (7):
    g0: ArcOfCircle CenterX=-3e-16 CenterY=10.15 CenterZ=0 NormalX=0 NormalY=0 NormalZ=1 AngleXU=0 Radius=9.5 StartAngle=5.9573 EndAngle=9.75066
    g1: LineSegment StartX=-9 StartY=7.10862 StartZ=0 EndX=-9 EndY=-14.15 EndZ=0
    g2: LineSegment StartX=-9 StartY=-14.15 StartZ=0 EndX=-5 EndY=-14.15 EndZ=0
    g3: LineSegment StartX=5 StartY=-14.15 StartZ=0 EndX=9 EndY=-14.15 EndZ=0
    g4: LineSegment StartX=9 StartY=-14.15 StartZ=0 EndX=9 EndY=7.10862 EndZ=0
    g5: ArcOfCircle CenterX=-3e-16 CenterY=-10.4 CenterZ=0 NormalX=0 NormalY=0 NormalZ=1 AngleXU=0 Radius=6.25 StartAngle=3.78509 EndAngle=5.63968
    g6: LineSegment [constr] StartX=0 StartY=-20.15 StartZ=0 EndX=0 EndY=-16.65 EndZ=0
  constraints (22):
    c: Symmetric(g0,g0,g-2)
    c: Coincident(g1,g0)
    c: Vertical(g1)
    c: Coincident(g2,g1)
    c: Horizontal(g2)
    c: Horizontal(g3)
    c: Coincident(g4,g3)
    c: Coincident(g4,g0)
    c: Vertical(g4)
    c: Symmetric(g2,g3,g-2)
    c: Coincident(g5,g2)
    c: Coincident(g5,g3)
    c: DistanceY(g-3,g3) = 6
    c: DistanceY(g0,g-4) = 10
    c: Radius(g0) = 9.5
    c: DistanceX(g0,g0) = 18
    c: PointOnObject(g6,g-3)
    c: PointOnObject(g6,g5)
    c: Vertical(g6)
    c: DistanceY(g6,g6) = 3.5
    c: DistanceX(g2,g3) = 10
    c: PointOnObject(g6,g-2)
FEATURE [PartDesign::Pad] Pad353
  BaseFeature = -> Pad351
  Length = 2.5
  Length2 = 100
  Profile = -> Sketch787
  Type = 0
FEATURE [Sketcher::SketchObject] Sketch773
  ExternalGeometry = -> [Pad353]
  MapMode = 5
  Placement = pos=(0,0,37.6) rot=(0,0,1;0rad)
  Support = -> [Pad353]
  sketch-geometry (1):
    g0: Circle CenterX=-3e-16 CenterY=10.15 CenterZ=0 NormalX=0 NormalY=0 NormalZ=1 AngleXU=0 Radius=6.5
  constraints (2):
    c: Coincident(g0,g-3)
    c: Radius(g0) = 6.5
FEATURE [PartDesign::Pad] Pad343
  BaseFeature = -> Pad353
  Length = 1
  Length2 = 100
  Profile = -> Sketch773
  Type = 0
FEATURE [Sketcher::SketchObject] Sketch761
  ExternalGeometry = -> [Pad343]
  MapMode = 5
  Placement = pos=(0,0,38.6) rot=(0,0,1;0rad)
  Support = -> [Pad343]
  sketch-geometry (1):
    g0: Circle CenterX=0 CenterY=10.15 CenterZ=0 NormalX=0 NormalY=0 NormalZ=1 AngleXU=0 Radius=5.5
  constraints (2):
    c: Coincident(g0,g-3)
    c: Radius(g0) = 5.5
FEATURE [PartDesign::Pad] Pad348
  BaseFeature = -> Pad343
  Length = 0.5
  Length2 = 100
  Profile = -> Sketch761
  Type = 0
FEATURE [Sketcher::SketchObject] Sketch791
  ExternalGeometry = -> [Pad348]
  MapMode = 5
  Placement = pos=(0,0,39.1) rot=(0,0,1;0rad)
  Support = -> [Pad348]
  sketch-geometry (1):
    g0: Circle CenterX=0 CenterY=10.15 CenterZ=0 NormalX=0 NormalY=0 NormalZ=1 AngleXU=0 Radius=3
  constraints (2):
    c: Coincident(g0,g-3)
    c: Radius(g0) = 3
FEATURE [PartDesign::Pad] Pad341
  BaseFeature = -> Pad348
  Length = 4
  Length2 = 100
  Profile = -> Sketch791
  Type = 0
FEATURE [Sketcher::SketchObject] Sketch800
  ExternalGeometry = -> [Pad341]
  MapMode = 5
  Placement = pos=(0,0,43.1) rot=(0,0,1;0rad)
  Support = -> [Pad341]
  sketch-geometry (1):
    g0: Circle CenterX=0 CenterY=10.15 CenterZ=0 NormalX=0 NormalY=0 NormalZ=1 AngleXU=0 Radius=1.5
  constraints (2):
    c: Coincident(g0,g-3)
    c: Radius(g0) = 1.5
FEATURE [PartDesign::Pocket] Pocket337
  BaseFeature = -> Pad341
  Length = 5
  Length2 = 100
  Profile = -> Sketch800
  Type = 0
FEATURE [Sketcher::SketchObject] Sketch777
  MapMode = 5
  Placement = pos=(0,0,29.1) rot=(0,0,1;0rad)
  Support = -> [Pocket337]
  sketch-geometry (4):
    g0: Circle CenterX=-4.91157 CenterY=25.3 CenterZ=0 NormalX=0 NormalY=0 NormalZ=1 AngleXU=0 Radius=2.25
    g1: Circle CenterX=4.91157 CenterY=25.3 CenterZ=0 NormalX=0 NormalY=0 NormalZ=1 AngleXU=0 Radius=2.25
    g2: Circle CenterX=-4.91157 CenterY=-25.3 CenterZ=0 NormalX=0 NormalY=0 NormalZ=1 AngleXU=0 Radius=2.25
    g3: Circle CenterX=4.91157 CenterY=-25.3 CenterZ=0 NormalX=0 NormalY=0 NormalZ=1 AngleXU=0 Radius=2.25
  constraints (8):
    c: Equal(g3,g2)
    c: Equal(g2,g1)
    c: Equal(g1,g0)
    c: Radius(g1) = 2.25
    c: Symmetric(g1,g0,g-2)
    c: Symmetric(g3,g2,g-2)
    c: Symmetric(g3,g1,g-1)
    c: DistanceY(g3,g1) = 50.6
FEATURE [PartDesign::Pocket] Pocket331
  BaseFeature = -> Pocket337
  Length = 5
  Length2 = 100
  Profile = -> Sketch777
  Type = 0
FEATURE [Sketcher::SketchObject] Sketch778
  MapMode = 5
  Placement = pos=(0,0,29.1) rot=(0,0,1;0rad)
  Support = -> [Pocket331]
  sketch-geometry (8):
    g0: LineSegment StartX=-0.5 StartY=26.8 StartZ=0 EndX=0.5 EndY=26.8 EndZ=0
    g1: LineSegment StartX=0.5 StartY=26.8 StartZ=0 EndX=0.5 EndY=20.15 EndZ=0
    g2: LineSegment StartX=0.5 StartY=20.15 StartZ=0 EndX=-0.5 EndY=20.15 EndZ=0
    g3: LineSegment StartX=-0.5 StartY=20.15 StartZ=0 EndX=-0.5 EndY=26.8 EndZ=0
    g4: LineSegment StartX=-0.5 StartY=-20.15 StartZ=0 EndX=0.5 EndY=-20.15 EndZ=0
    g5: LineSegment StartX=0.5 StartY=-20.15 StartZ=0 EndX=0.5 EndY=-26.8 EndZ=0
    g6: LineSegment StartX=0.5 StartY=-26.8 StartZ=0 EndX=-0.5 EndY=-26.8 EndZ=0
    g7: LineSegment StartX=-0.5 StartY=-26.8 StartZ=0 EndX=-0.5 EndY=-20.15 EndZ=0
  constraints (20):
    c: Coincident(g0,g1)
    c: Coincident(g1,g2)
    c: Coincident(g2,g3)
    c: Coincident(g3,g0)
    c: Horizontal(g2)
    c: Vertical(g1)
    c: Vertical(g3)
    c: Coincident(g4,g5)
    c: Coincident(g5,g6)
    c: Coincident(g6,g7)
    c: Coincident(g7,g4)
    c: Horizontal(g6)
    c: Vertical(g7)
    c: Symmetric(g4,g4,g-2)
    c: Symmetric(g0,g0,g-2)
    c: Symmetric(g0,g5,g-1)
    c: DistanceY(g5,g0) = 53.6
    c: DistanceY(g4,g1) = 40.3
    c: DistanceX(g0,g0) = 1
    c: Symmetric(g4,g1,g-1)
FEATURE [PartDesign::Pad] Pad355
  BaseFeature = -> Pocket331
  Length = 2
  Length2 = 100
  Profile = -> Sketch778
  Type = 0
FEATURE [Sketcher::SketchObject] Sketch801
  ExternalGeometry = -> [Pad355]
  MapMode = 5
  Placement = pos=(0.5,0,0) rot=(0.57735,0.57735,0.57735;2.0944rad)
  Support = -> [Pad355]
  sketch-geometry (6):
    g0: LineSegment StartX=-26.8 StartY=29.1 StartZ=0 EndX=-26.8 EndY=31.1 EndZ=0
    g1: LineSegment StartX=-26.8 StartY=31.1 StartZ=0 EndX=-20.15 EndY=31.1 EndZ=0
    g2: LineSegment StartX=-20.15 StartY=31.1 StartZ=0 EndX=-26.8 EndY=29.1 EndZ=0
    g3: LineSegment StartX=20.15 StartY=31.1 StartZ=0 EndX=26.8 EndY=31.1 EndZ=0
    g4: LineSegment StartX=26.8 StartY=31.1 StartZ=0 EndX=26.8 EndY=29.1 EndZ=0
    g5: LineSegment StartX=26.8 StartY=29.1 StartZ=0 EndX=20.15 EndY=31.1 EndZ=0
  constraints (14):
    c: Vertical(g0)
    c: Coincident(g0,g1)
    c: Horizontal(g1)
    c: Coincident(g1,g2)
    c: Coincident(g2,g0)
    c: Coincident(g3,g4)
    c: Coincident(g4,g5)
    c: Coincident(g5,g3)
    c: Symmetric(g0,g4,g-2)
    c: Symmetric(g3,g0,g-2)
    c: Symmetric(g1,g3,g-2)
    c: DistanceX(g0,g3) = 53.6
    c: DistanceY(g4,g4) = 2
    c: Coincident(g3,g-3)
FEATURE [PartDesign::Pocket] Pocket338
  BaseFeature = -> Pad355
  Length = 1
  Length2 = 100
  Profile = -> Sketch801
  Type = 0
FEATURE [PartDesign::Fillet] Fillet107
  Base = -> Pocket338 [Edge26,Edge27,Edge72,Edge63,Edge70,Edge78,Edge51,Edge49,Edge71,Edge50,Edge79,Edge86,Edge30,Edge21,Edge4,Edge29,Edge105,Edge107,Edge109,Edge111,Edge113,Edge114,Edge123]
  BaseFeature = -> Pocket338
  Radius = 0.4
FEATURE [Sketcher::SketchObject] Sketch789
  MapMode = 5
  Placement = pos=(0,20.15,0) rot=(0,0.707107,0.707107;3.14159rad)
  Support = -> [Fillet107]
  sketch-geometry (4):
    g0: LineSegment StartX=-3.25 StartY=2 StartZ=0 EndX=3.25 EndY=2 EndZ=0
    g1: LineSegment StartX=3.25 StartY=2 StartZ=0 EndX=3.25 EndY=6 EndZ=0
    g2: LineSegment StartX=3.25 StartY=6 StartZ=0 EndX=-3.25 EndY=6 EndZ=0
    g3: LineSegment StartX=-3.25 StartY=6 StartZ=0 EndX=-3.25 EndY=2 EndZ=0
  constraints (11):
    c: Coincident(g0,g1)
    c: Coincident(g1,g2)
    c: Coincident(g2,g3)
    c: Coincident(g3,g0)
    c: Horizontal(g0)
    c: Vertical(g1)
    c: Vertical(g3)
    c: DistanceY(g-1,g0) = 2
    c: DistanceY(g1,g1) = 4
    c: Symmetric(g2,g1,g-2)
    c: DistanceX(g2,g2) = 6.5
FEATURE [PartDesign::Pad] Pad352
  BaseFeature = -> Fillet107
  Length = 1
  Length2 = 100
  Profile = -> Sketch789
  Type = 0
FEATURE [Sketcher::SketchObject] Sketch785
  MapMode = 5
  Placement = pos=(0,21.15,0) rot=(0,0.707107,0.707107;3.14159rad)
  Support = -> [Pad352]
  sketch-geometry (4):
    g0: LineSegment StartX=-2.75 StartY=5.5 StartZ=0 EndX=2.75 EndY=5.5 EndZ=0
    g1: LineSegment StartX=2.75 StartY=5.5 StartZ=0 EndX=2.75 EndY=2.5 EndZ=0
    g2: LineSegment StartX=2.75 StartY=2.5 StartZ=0 EndX=-2.75 EndY=2.5 EndZ=0
    g3: LineSegment StartX=-2.75 StartY=2.5 StartZ=0 EndX=-2.75 EndY=5.5 EndZ=0
  constraints (11):
    c: Coincident(g0,g1)
    c: Coincident(g1,g2)
    c: Coincident(g2,g3)
    c: Coincident(g3,g0)
    c: Horizontal(g0)
    c: Vertical(g1)
    c: Vertical(g3)
    c: Symmetric(g1,g2,g-2)
    c: DistanceY(g1,g0) = 3
    c: DistanceY(g-1,g1) = 2.5
    c: DistanceX(g0,g0) = 5.5
FEATURE [PartDesign::Pad] Pad331
  BaseFeature = -> Pad352
  Length = 4
  Length2 = 100
  Profile = -> Sketch785
  Type = 0
FEATURE [Sketcher::SketchObject] Sketch776
  MapMode = 5
  Placement = pos=(0,0,0) rot=(1,0,0;3.14159rad)
  Support = -> [Pad331]
  sketch-geometry (4):
    g0: LineSegment StartX=-10 StartY=-20.15 StartZ=0 EndX=10 EndY=-20.15 EndZ=0
    g1: LineSegment StartX=10 StartY=-20.15 StartZ=0 EndX=10 EndY=20.15 EndZ=0
    g2: LineSegment StartX=10 StartY=20.15 StartZ=0 EndX=-10 EndY=20.15 EndZ=0
    g3: LineSegment StartX=-10 StartY=20.15 StartZ=0 EndX=-10 EndY=-20.15 EndZ=0
  constraints (10):
    c: Coincident(g0,g1)
    c: Coincident(g1,g2)
    c: Coincident(g2,g3)
    c: Coincident(g3,g0)
    c: Horizontal(g0)
    c: Vertical(g1)
    c: Symmetric(g2,g1,g-2)
    c: Symmetric(g0,g2,g-1)
    c: DistanceX(g2,g2) = 20
    c: DistanceY(g1,g1) = 40.3
FEATURE [PartDesign::Pad] Pad354
  BaseFeature = -> Pad331
  Length = 2
  Length2 = 100
  Profile = -> Sketch776
  Type = 0
FEATURE [PartDesign::Chamfer] Chamfer187
  Base = -> Pad354 [Face7]
  BaseFeature = -> Pad354
  Size = 1.5
FEATURE [PartDesign::Fillet] Fillet114
  Base = -> Chamfer187 [Edge1,Edge7,Edge18,Edge4,Face12]
  BaseFeature = -> Chamfer187
  Radius = 0.4
FEATURE [Sketcher::SketchObject] Sketch762
  ExternalGeometry = -> [Fillet114]
  MapMode = 5
  Placement = pos=(0,0,43.1) rot=(0,0,1;0rad)
  Support = -> [Fillet114]
  sketch-geometry (1):
    g0: Circle CenterX=0 CenterY=10.15 CenterZ=0 NormalX=0 NormalY=0 NormalZ=1 AngleXU=0 Radius=3
  constraints (2):
    c: Coincident(g0,g-3)
    c: Radius(g0) = 3
FEATURE [PartDesign::Pocket] Pocket336
  BaseFeature = -> Fillet114
  Length = 5
  Length2 = 100
  Profile = -> Sketch762
  Type = 0
FEATURE [PartDesign::Body] Body214  label="MG996R006"
  Group = -> [Sketch802,Pad326,Sketch779,Pad356,Sketch784,Pad351,Sketch787,Pad353,Sketch773,Pad343,Sketch761,Pad348,Sketch791,Pad341,Sketch800,Pocket337,Sketch777,Pocket331,Sketch778,Pad355,Sketch801,Pocket338,Fillet107,Sketch789,Pad352,Sketch785,Pad331,Sketch776,Pad354,Chamfer187,Fillet114,Sketch762,Pocket336]
  Origin = -> Origin357
  Tip = -> Pocket336
FEATURE [App::Part] Part104  label="Servo007"
  Group = -> [Body214,Body189,Body176,Body225,Body212]
  Origin = -> Origin368
  Placement = pos=(-75.5841,15.8,113.841) rot=(-0.862856,0.357407,-0.357407;4.56541rad)
FEATURE [Sketcher::SketchObject] Sketch804
  ExternalGeometry = -> [Pad337]
  MapMode = 5
  Placement = pos=(0,0,0) rot=(0.57735,0.57735,0.57735;2.0944rad)
  Support = -> [YZ_Plane290]
  sketch-geometry (6):
    g0: LineSegment StartX=-2.67543 StartY=1.2 StartZ=0 EndX=-3.67543 EndY=1.2 EndZ=0
    g1: LineSegment StartX=-3.67543 StartY=1.2 StartZ=0 EndX=-3.67543 EndY=-1.2 EndZ=0
    g2: LineSegment StartX=-3.67543 StartY=-1.2 StartZ=0 EndX=-2.67543 EndY=-1.2 EndZ=0
    g3: LineSegment StartX=-2.67543 StartY=-1.2 StartZ=0 EndX=-3.17543 EndY=-1 EndZ=0
    g4: LineSegment StartX=-3.17543 StartY=-1 StartZ=0 EndX=-3.17543 EndY=1 EndZ=0
    g5: LineSegment StartX=-3.17543 StartY=1 StartZ=0 EndX=-2.67543 EndY=1.2 EndZ=0
  constraints (15):
    c: Horizontal(g0)
    c: Coincident(g0,g1)
    c: Coincident(g1,g2)
    c: Coincident(g2,g3)
    c: Coincident(g3,g4)
    c: Coincident(g4,g5)
    c: Coincident(g5,g0)
    c: Symmetric(g4,g3,g-1)
    c: Symmetric(g0,g2,g-1)
    c: Symmetric(g1,g0,g-1)
    c: DistanceX(g0,g4) = 0.5
    c: DistanceY(g3,g4) = 2
    c: DistanceY(g1,g0) = 2.4
    c: PointOnObject(g3,g-3)
    c: DistanceX(g4,g0) = 0.5
FEATURE [PartDesign::Groove] Groove070  label="M3 Nut Smooth066"
  Angle = 360
  Axis = (-2e-16,3e-16,1)
  Base = (0,0,0)
  BaseFeature = -> Pad337
  Profile = -> Sketch804
  ReferenceAxis = -> Sketch804 [V_Axis]
  Reversed = true
FEATURE [PartDesign::Chamfer] Chamfer181  label="M3 Nut Smooth Hole075"
  Base = -> Groove070 [Edge24,Edge23]
  BaseFeature = -> Groove070
  Size = 0.2
FEATURE [PartDesign::Body] Body199  label="M3 Nut034"
  Group = -> [Sketch793,Pad337,Sketch804,Groove070,Chamfer181]
  Origin = -> Origin346
  Placement = pos=(-138.956,-150.5,84.9639) rot=(0.862856,-0.357407,0.357407;1.71777rad)
  Tip = -> Chamfer181
FEATURE [Sketcher::SketchObject] Sketch805
  MapMode = 5
  Support = -> [XY_Plane272]
  sketch-geometry (1):
    g0: Circle CenterX=0 CenterY=0 CenterZ=0 NormalX=0 NormalY=0 NormalZ=1 AngleXU=0 Radius=2.75
  constraints (2):
    c: Coincident(g0,g-1)
    c: Radius(g0) = 2.75
FEATURE [PartDesign::Pad] Pad347  label="M3x20 Head027"
  Length = 3
  Length2 = 100
  Profile = -> Sketch805
  Type = 0
FEATURE [Sketcher::SketchObject] Sketch781
  MapMode = 5
  Placement = pos=(0,0,3) rot=(0,0,1;0rad)
  Support = -> [Pad347]
  sketch-geometry (1):
    g0: Circle CenterX=0 CenterY=0 CenterZ=0 NormalX=0 NormalY=0 NormalZ=1 AngleXU=0 Radius=1.5
  constraints (2):
    c: Coincident(g0,g-1)
    c: Radius(g0) = 1.5
FEATURE [PartDesign::Pad] Pad342  label="M3x20 Thread026"
  BaseFeature = -> Pad347
  Length = 20
  Length2 = 100
  Profile = -> Sketch781
  Type = 0
FEATURE [Sketcher::SketchObject] Sketch763
  MapMode = 5
  Placement = pos=(0,0,0) rot=(1,0,0;3.14159rad)
  Support = -> [Pad342]
  sketch-geometry (7):
    g0: LineSegment StartX=1.275 StartY=0.736122 StartZ=0 EndX=0 EndY=1.47224 EndZ=0
    g1: LineSegment StartX=0 StartY=1.47224 StartZ=0 EndX=-1.275 EndY=0.736122 EndZ=0
    g2: LineSegment StartX=-1.275 StartY=0.736122 StartZ=0 EndX=-1.275 EndY=-0.736122 EndZ=0
    g3: LineSegment StartX=-1.275 StartY=-0.736122 StartZ=0 EndX=1.34766e-11 EndY=-1.47224 EndZ=0
    g4: LineSegment StartX=1.34766e-11 StartY=-1.47224 StartZ=0 EndX=1.275 EndY=-0.736122 EndZ=0
    g5: LineSegment StartX=1.275 StartY=-0.736122 StartZ=0 EndX=1.275 EndY=0.736122 EndZ=0
    g6: Circle [constr] CenterX=0 CenterY=0 CenterZ=0 NormalX=0 NormalY=0 NormalZ=1 AngleXU=0 Radius=1.47224
  constraints (16):
    c: Coincident(g0,g1)
    c: Coincident(g1,g2)
    c: Coincident(g2,g3)
    c: Coincident(g3,g4)
    c: Coincident(g4,g5)
    c: Coincident(g5,g0)
    c: Equal(g0, g1-g5) x5
    c: PointOnObject(g0,g6)
    c: PointOnObject(g1,g6)
    c: PointOnObject(g2,g6)
    c: PointOnObject(g3,g6)
    c: PointOnObject(g4,g6)
    c: PointOnObject(g5,g6)
    c: Coincident(g6,g-1)
    c: PointOnObject(g0,g-2)
    c: DistanceX(g1,g0) = 2.55
FEATURE [PartDesign::Pocket] Pocket321  label="M3x20 Wrench025"
  BaseFeature = -> Pad342
  Length = 1.3
  Length2 = 100
  Profile = -> Sketch763
  Type = 0
FEATURE [PartDesign::Chamfer] Chamfer185  label="M3x20 Smooth033"
  Base = -> Pocket321 [Face11,Edge2,Edge24,Edge3]
  BaseFeature = -> Pocket321
  Size = 0.2
FEATURE [PartDesign::Body] Body229  label="M3x054"
  Group = -> [Sketch805,Pad347,Sketch781,Pad342,Sketch763,Pocket321,Chamfer185]
  Origin = -> Origin323
  Placement = pos=(-121.75,-30,34) rot=(-1,0,0;1.5708rad)
  Tip = -> Chamfer185
FEATURE [Sketcher::SketchObject] Sketch806
  MapMode = 5
  Support = -> [XY_Plane281]
  sketch-geometry (9):
    g0: LineSegment StartX=-2.8e-15 StartY=0 StartZ=0 EndX=56.5 EndY=0 EndZ=0
    g1: LineSegment StartX=56.5 StartY=0 StartZ=0 EndX=56.5 EndY=25 EndZ=0
    g2: LineSegment StartX=51.5 StartY=30 StartZ=0 EndX=-80 EndY=30 EndZ=0
    g3: ArcOfCircle CenterX=-80 CenterY=15 CenterZ=0 NormalX=0 NormalY=0 NormalZ=1 AngleXU=0 Radius=15 StartAngle=1.5708 EndAngle=5.50197
    g4: ArcOfCircle CenterX=-50 CenterY=-14.75 CenterZ=0 NormalX=0 NormalY=0 NormalZ=1 AngleXU=0 Radius=27.25 StartAngle=1.5708 EndAngle=2.36038
    g5: ArcOfCircle CenterX=-30 CenterY=-14.75 CenterZ=0 NormalX=0 NormalY=0 NormalZ=1 AngleXU=0 Radius=27.25 StartAngle=0.781214 EndAngle=1.5708
    g6: ArcOfCircle CenterX=0 CenterY=15 CenterZ=0 NormalX=0 NormalY=0 NormalZ=1 AngleXU=0 Radius=15 StartAngle=3.92281 EndAngle=4.71239
    g7: LineSegment StartX=-50 StartY=12.5 StartZ=0 EndX=-30 EndY=12.5 EndZ=0
    g8: ArcOfCircle CenterX=51.5 CenterY=25 CenterZ=0 NormalX=0 NormalY=0 NormalZ=1 AngleXU=0 Radius=5 StartAngle=3e-16 EndAngle=1.5708
  constraints (23):
    c: Coincident(g0,g1)
    c: Horizontal(g0)
    c: Horizontal(g2)
    c: Vertical(g1)
    c: DistanceX(g0,g0) = 56.5
    c: Horizontal(g7)
    c: Radius(g3) = 15
    c: Tangent(g7,g5) = 1.5708
    c: Tangent(g4,g3) = 1.5708
    c: Tangent(g3,g2) = -1.5708
    c: Tangent(g7,g4) = 1.5708
    c: Tangent(g6,g5) = 1.5708
    c: Tangent(g6,g0) = -1.5708
    c: Equal(g3,g6)
    c: Equal(g4,g5)
    c: DistanceY(g0,g5) = 12.5
    c: DistanceX(g2,g0) = 80
    c: DistanceX(g4,g5) = 20
    c: Tangent(g3,g-1)
    c: Tangent(g2,g8) = -1.5708
    c: Tangent(g1,g8) = -1.5708
    c: Radius(g8) = 5
    c: Coincident(g0,g-1)
FEATURE [PartDesign::Pad] Pad311  label="Baseplate015"
  Length = 20
  Length2 = 100
  Profile = -> Sketch806
  Type = 0
FEATURE [Sketcher::SketchObject] Sketch810
  ExternalGeometry = -> [Pad311]
  MapMode = 5
  Placement = pos=(0,0,20) rot=(0,0,1;0rad)
  Support = -> [Pad311]
  sketch-geometry (18):
    g0: LineSegment StartX=-87.0711 StartY=22.0711 StartZ=0 EndX=-72.9287 EndY=7.92875 EndZ=0
    g1: LineSegment StartX=-50 StartY=17.1099 StartZ=0 EndX=-30 EndY=17.1099 EndZ=0
    g2: LineSegment StartX=-30 StartY=17.1099 StartZ=0 EndX=-30 EndY=25 EndZ=0
    g3: LineSegment StartX=-30 StartY=25 StartZ=0 EndX=-50 EndY=25 EndZ=0
    g4: LineSegment StartX=-50 StartY=25 StartZ=0 EndX=-50 EndY=17.1099 EndZ=0
    g5: LineSegment StartX=-55 StartY=25 StartZ=0 EndX=-55 EndY=17.1099 EndZ=0
    g6: LineSegment StartX=-55 StartY=25 StartZ=0 EndX=-80 EndY=25 EndZ=0
    g7: LineSegment StartX=-25 StartY=25 StartZ=0 EndX=-25 EndY=17.1099 EndZ=0
    g8: ArcOfCircle CenterX=-80 CenterY=15 CenterZ=0 NormalX=0 NormalY=0 NormalZ=1 AngleXU=0 Radius=10 StartAngle=1.5708 EndAngle=2.35619
    g9: ArcOfCircle CenterX=-50 CenterY=-14.75 CenterZ=0 NormalX=0 NormalY=0 NormalZ=1 AngleXU=0 Radius=32.2499 StartAngle=1.72646 EndAngle=2.36168
    g10: ArcOfCircle CenterX=-30 CenterY=-14.75 CenterZ=0 NormalX=0 NormalY=0 NormalZ=1 AngleXU=0 Radius=32.2499 StartAngle=0.781214 EndAngle=1.41513
    g11: ArcOfCircle CenterX=0 CenterY=15 CenterZ=0 NormalX=0 NormalY=0 NormalZ=1 AngleXU=0 Radius=10.0001 StartAngle=3.92281 EndAngle=4.1888
    g12: LineSegment StartX=-25 StartY=25 StartZ=0 EndX=-5 EndY=25 EndZ=0
    g13: LineSegment StartX=-5 StartY=25 StartZ=0 EndX=-5 EndY=6.33958 EndZ=0
    g14: LineSegment StartX=8 StartY=25 StartZ=0 EndX=48.5 EndY=25 EndZ=0
    g15: LineSegment StartX=48.5 StartY=25 StartZ=0 EndX=48.5 EndY=5 EndZ=0
    g16: LineSegment StartX=48.5 StartY=5 StartZ=0 EndX=8 EndY=5 EndZ=0
    g17: LineSegment StartX=8 StartY=5 StartZ=0 EndX=8 EndY=25 EndZ=0
  constraints (52):
    c: Coincident(g1,g2)
    c: Coincident(g2,g3)
    c: Coincident(g3,g4)
    c: Coincident(g4,g1)
    c: Horizontal(g1)
    c: Horizontal(g3)
    c: Vertical(g2)
    c: Vertical(g4)
    c: Coincident(g6,g5)
    c: Horizontal(g6)
    c: Vertical(g7)
    c: Vertical(g5)
    c: Coincident(g8,g0)
    c: Coincident(g9,g5)
    c: Coincident(g10,g7)
    c: Coincident(g12,g7)
    c: Horizontal(g12)
    c: Tangent(g8,g6) = -1.5708
    c: Horizontal(g5,g3)
    c: Horizontal(g2,g7)
    c: Horizontal(g1,g7)
    c: Horizontal(g5,g1)
    c: Tangent(g11,g10) = 1.5708
    c: Angle(g0) = -0.785398
    c: Radius(g8) = 10
    c: Coincident(g8,g-3)
    c: PointOnObject(g8,g0)
    c: Coincident(g9,g0)
    c: DistanceX(g5,g3) = 5
    c: DistanceX(g2,g7) = 5
    c: DistanceX(g11,g-1) = 5
    c: Coincident(g13,g12)
    c: Coincident(g13,g11)
    c: Vertical(g13)
    c: Coincident(g-4,g9)
    c: Coincident(g10,g-5)
    c: Distance(g0,g-4) = 5
    c: Coincident(g11,g-6)
    c: Vertical(g-4,g1)
    c: Vertical(g-5,g1)
    c: Coincident(g14,g15)
    c: Coincident(g15,g16)
    c: Coincident(g16,g17)
    c: Coincident(g17,g14)
    c: Horizontal(g14)
    c: Horizontal(g16)
    c: Vertical(g15)
    c: Vertical(g17)
    c: DistanceX(g-1,g16) = 8
    c: DistanceY(g-1,g16) = 5
    c: DistanceX(g14,g14) = 40.5
    c: DistanceY(g15,g15) = 20
FEATURE [PartDesign::Pocket] Pocket320  label="Leg and Servo Pockets001"
  BaseFeature = -> Pad311
  Length = 20
  Length2 = 100
  Profile = -> Sketch810
  Type = 0
FEATURE [PartDesign::Fillet] Fillet111  label="Smooth Leg Pockets001"
  Base = -> Pocket320 [Edge76,Edge72,Edge73,Edge75,Edge69,Edge70,Edge71,Edge68,Edge77,Edge81,Edge79,Edge80]
  BaseFeature = -> Pocket320
  Radius = 2
FEATURE [Sketcher::SketchObject] Sketch799
  MapMode = 5
  Placement = pos=(0,0,20) rot=(0,0,1;0rad)
  Support = -> [Fillet111]
  sketch-geometry (4):
    g0: LineSegment StartX=0 StartY=0 StartZ=0 EndX=56.5 EndY=0 EndZ=0
    g1: LineSegment StartX=56.5 StartY=0 StartZ=0 EndX=56.5 EndY=25 EndZ=0
    g2: LineSegment StartX=56.5 StartY=25 StartZ=0 EndX=0 EndY=25 EndZ=0
    g3: LineSegment StartX=0 StartY=25 StartZ=0 EndX=0 EndY=0 EndZ=0
  constraints (11):
    c: Coincident(g0,g1)
    c: Coincident(g1,g2)
    c: Coincident(g2,g3)
    c: Coincident(g3,g0)
    c: Horizontal(g0)
    c: Horizontal(g2)
    c: Vertical(g1)
    c: Vertical(g3)
    c: Coincident(g0,g-1)
    c: DistanceY(g3,g3) = 25
    c: DistanceX(g2,g2) = 56.5
FEATURE [PartDesign::Pocket] Pocket306  label="Counterpart Pocket001"
  BaseFeature = -> Fillet111
  Length = 10
  Length2 = 100
  Profile = -> Sketch799
  Type = 0
FEATURE [PartDesign::Pad] Pad312  label="Extend Baseplate001"
  BaseFeature = -> Pocket306
  Length = 12
  Length2 = 100
  Profile = -> Pocket306 [Face40]
  Type = 0
FEATURE [Sketcher::SketchObject] Sketch812
  MapMode = 5
  Placement = pos=(0,0,3) rot=(0,0,1;0rad)
  Support = -> [Pad334]
  sketch-geometry (1):
    g0: Circle CenterX=0 CenterY=0 CenterZ=0 NormalX=0 NormalY=0 NormalZ=1 AngleXU=0 Radius=1.5
  constraints (2):
    c: Coincident(g0,g-1)
    c: Radius(g0) = 1.5
FEATURE [PartDesign::Pad] Pad316  label="M3x20 Thread024"
  BaseFeature = -> Pad334
  Length = 20
  Length2 = 100
  Profile = -> Sketch812
  Type = 0
FEATURE [Sketcher::SketchObject] Sketch807
  MapMode = 5
  Placement = pos=(0,0,0) rot=(1,0,0;3.14159rad)
  Support = -> [Pad316]
  sketch-geometry (7):
    g0: LineSegment StartX=1.275 StartY=0.736122 StartZ=0 EndX=0 EndY=1.47224 EndZ=0
    g1: LineSegment StartX=0 StartY=1.47224 StartZ=0 EndX=-1.275 EndY=0.736122 EndZ=0
    g2: LineSegment StartX=-1.275 StartY=0.736122 StartZ=0 EndX=-1.275 EndY=-0.736122 EndZ=0
    g3: LineSegment StartX=-1.275 StartY=-0.736122 StartZ=0 EndX=1.34766e-11 EndY=-1.47224 EndZ=0
    g4: LineSegment StartX=1.34766e-11 StartY=-1.47224 StartZ=0 EndX=1.275 EndY=-0.736122 EndZ=0
    g5: LineSegment StartX=1.275 StartY=-0.736122 StartZ=0 EndX=1.275 EndY=0.736122 EndZ=0
    g6: Circle [constr] CenterX=0 CenterY=0 CenterZ=0 NormalX=0 NormalY=0 NormalZ=1 AngleXU=0 Radius=1.47224
  constraints (16):
    c: Coincident(g0,g1)
    c: Coincident(g1,g2)
    c: Coincident(g2,g3)
    c: Coincident(g3,g4)
    c: Coincident(g4,g5)
    c: Coincident(g5,g0)
    c: Equal(g0, g1-g5) x5
    c: PointOnObject(g0,g6)
    c: PointOnObject(g1,g6)
    c: PointOnObject(g2,g6)
    c: PointOnObject(g3,g6)
    c: PointOnObject(g4,g6)
    c: PointOnObject(g5,g6)
    c: Coincident(g6,g-1)
    c: PointOnObject(g0,g-2)
    c: DistanceX(g1,g0) = 2.55
FEATURE [PartDesign::Pocket] Pocket317  label="M3x20 Wrench024"
  BaseFeature = -> Pad316
  Length = 1.3
  Length2 = 100
  Profile = -> Sketch807
  Type = 0
FEATURE [PartDesign::Chamfer] Chamfer186  label="M3x20 Smooth034"
  Base = -> Pocket317 [Face11,Edge2,Edge24,Edge3]
  BaseFeature = -> Pocket317
  Size = 0.2
FEATURE [PartDesign::Body] Body226  label="M3x052"
  Group = -> [Sketch794,Pad334,Sketch812,Pad316,Sketch807,Pocket317,Chamfer186]
  Origin = -> Origin336
  Placement = pos=(-149,-30,75) rot=(-1,0,0;1.5708rad)
  Tip = -> Chamfer186
FEATURE [Sketcher::SketchObject] Sketch813
  MapMode = 5
  Placement = pos=(0,0,0) rot=(1,0,0;1.5708rad)
  Support = -> [XZ_Plane286]
  sketch-geometry (2):
    g0: ArcOfCircle CenterX=0 CenterY=0 CenterZ=0 NormalX=0 NormalY=0 NormalZ=1 AngleXU=0 Radius=20 StartAngle=-1.8e-15 EndAngle=3.14159
    g1: LineSegment StartX=-20 StartY=-1.38798e-11 StartZ=0 EndX=20 EndY=-3.55e-14 EndZ=0
  constraints (6):
    c: Coincident(g0,g-1)
    c: PointOnObject(g0,g-1)
    c: PointOnObject(g0,g-1)
    c: Coincident(g1,g0)
    c: Coincident(g1,g0)
    c: Radius(g0) = 20
FEATURE [PartDesign::Pad] Pad315  label="Baseblock006"
  Length = 15
  Length2 = 15
  Placement = pos=(0,0,0) rot=(1,0,0;1.5708rad)
  Profile = -> Sketch813
  Type = 4
FEATURE [Sketcher::SketchObject] Sketch814
  MapMode = 5
  Placement = pos=(0,0,0) rot=(1,0,0;1.5708rad)
  Support = -> [XZ_Plane286]
  sketch-geometry (2):
    g0: Circle [constr] CenterX=0 CenterY=0 CenterZ=0 NormalX=0 NormalY=0 NormalZ=1 AngleXU=0 Radius=20
    g1: Circle CenterX=-20 CenterY=0 CenterZ=0 NormalX=0 NormalY=0 NormalZ=1 AngleXU=0 Radius=1.25
  constraints (5):
    c: Coincident(g0,g-1)
    c: Radius(g0) = 20
    c: PointOnObject(g1,g0)
    c: Radius(g1) = 1.25
    c: PointOnObject(g1,g-1)
FEATURE [Sketcher::SketchObject] Sketch817
  MapMode = 5
  Placement = pos=(0,0,0) rot=(1,0,0;3.14159rad)
  Support = -> [Pad335]
  sketch-geometry (7):
    g0: LineSegment StartX=1.275 StartY=0.736122 StartZ=0 EndX=0 EndY=1.47224 EndZ=0
    g1: LineSegment StartX=0 StartY=1.47224 StartZ=0 EndX=-1.275 EndY=0.736122 EndZ=0
    g2: LineSegment StartX=-1.275 StartY=0.736122 StartZ=0 EndX=-1.275 EndY=-0.736122 EndZ=0
    g3: LineSegment StartX=-1.275 StartY=-0.736122 StartZ=0 EndX=1.34766e-11 EndY=-1.47224 EndZ=0
    g4: LineSegment StartX=1.34766e-11 StartY=-1.47224 StartZ=0 EndX=1.275 EndY=-0.736122 EndZ=0
    g5: LineSegment StartX=1.275 StartY=-0.736122 StartZ=0 EndX=1.275 EndY=0.736122 EndZ=0
    g6: Circle [constr] CenterX=0 CenterY=0 CenterZ=0 NormalX=0 NormalY=0 NormalZ=1 AngleXU=0 Radius=1.47224
  constraints (16):
    c: Coincident(g0,g1)
    c: Coincident(g1,g2)
    c: Coincident(g2,g3)
    c: Coincident(g3,g4)
    c: Coincident(g4,g5)
    c: Coincident(g5,g0)
    c: Equal(g0, g1-g5) x5
    c: PointOnObject(g0,g6)
    c: PointOnObject(g1,g6)
    c: PointOnObject(g2,g6)
    c: PointOnObject(g3,g6)
    c: PointOnObject(g4,g6)
    c: PointOnObject(g5,g6)
    c: Coincident(g6,g-1)
    c: PointOnObject(g0,g-2)
    c: DistanceX(g1,g0) = 2.55
FEATURE [PartDesign::Pocket] Pocket327  label="M3x20 Wrench027"
  BaseFeature = -> Pad335
  Length = 1.3
  Length2 = 100
  Profile = -> Sketch817
  Type = 0
FEATURE [PartDesign::Chamfer] Chamfer183  label="M3x20 Smooth032"
  Base = -> Pocket327 [Face11,Edge2,Edge24,Edge3]
  BaseFeature = -> Pocket327
  Size = 0.2
FEATURE [PartDesign::Body] Body231  label="M3x055"
  Group = -> [Sketch792,Pad333,Sketch796,Pad335,Sketch817,Pocket327,Chamfer183]
  Origin = -> Origin356
  Placement = pos=(-156,-30,68) rot=(-1,0,0;1.5708rad)
  Tip = -> Chamfer183
FEATURE [App::Part] Part090  label="m3x20 screws001"
  Group = -> [Body226,Body231,Body229,Body227]
  Origin = -> Origin329
  Placement = pos=(59.5,12.25,59.5) rot=(0,0,1;0rad)
FEATURE [Sketcher::SketchObject] Sketch819
  MapMode = 5
  Placement = pos=(0,0,32) rot=(0,0,1;0rad)
  Support = -> [Pad312]
  sketch-geometry (4):
    g0: LineSegment StartX=48.5 StartY=25 StartZ=0 EndX=56.5 EndY=25 EndZ=0
    g1: LineSegment StartX=56.5 StartY=25 StartZ=0 EndX=56.5 EndY=30 EndZ=0
    g2: LineSegment StartX=56.5 StartY=30 StartZ=0 EndX=48.5 EndY=30 EndZ=0
    g3: LineSegment StartX=48.5 StartY=30 StartZ=0 EndX=48.5 EndY=25 EndZ=0
  constraints (12):
    c: Coincident(g0,g1)
    c: Coincident(g1,g2)
    c: Coincident(g2,g3)
    c: Coincident(g3,g0)
    c: Horizontal(g0)
    c: Horizontal(g2)
    c: Vertical(g1)
    c: Vertical(g3)
    c: DistanceY(g3,g3) = 5
    c: DistanceY(g-1,g0) = 25
    c: DistanceX(g2,g2) = 8
    c: DistanceX(g-1,g2) = 48.5
FEATURE [PartDesign::Pocket] Pocket302  label="Remove Extension Servocover001"
  BaseFeature = -> Pad312
  Length = 13
  Length2 = 100
  Profile = -> Sketch819
  Type = 0
FEATURE [Sketcher::SketchObject] Sketch808
  MapMode = 5
  Placement = pos=(0,30,0) rot=(0,0.707107,0.707107;3.14159rad)
  Support = -> [Pocket302]
  sketch-geometry (7):
    g0: ArcOfCircle CenterX=22.5 CenterY=65.1875 CenterZ=0 NormalX=0 NormalY=0 NormalZ=1 AngleXU=0 Radius=45.1875 StartAngle=4.19118 EndAngle=4.71239
    g1: LineSegment StartX=-56.5 StartY=33 StartZ=0 EndX=95 EndY=33 EndZ=0
    g2: LineSegment StartX=95 StartY=33 StartZ=0 EndX=95 EndY=20 EndZ=0
    g3: LineSegment StartX=95 StartY=20 StartZ=0 EndX=22.5 EndY=20 EndZ=0
    g4: ArcOfCircle CenterX=-22.5 CenterY=-13.1875 CenterZ=0 NormalX=0 NormalY=0 NormalZ=1 AngleXU=0 Radius=45.1875 StartAngle=1.04959 EndAngle=1.5708
    g5: LineSegment StartX=-22.5 StartY=32 StartZ=0 EndX=-56.5 EndY=32 EndZ=0
    g6: LineSegment StartX=-56.5 StartY=32 StartZ=0 EndX=-56.5 EndY=33 EndZ=0
  constraints (21):
    c: Horizontal(g1)
    c: Coincident(g2,g1)
    c: Vertical(g2)
    c: Coincident(g3,g2)
    c: Horizontal(g3)
    c: Tangent(g3,g0) = 1.5708
    c: DistanceX(g0,g0) = 22.5
    c: DistanceY(g0,g1) = 7
    c: DistanceY(g2,g2) = 13
    c: PointOnObject(g0,g-2)
    c: DistanceY(g-1,g2) = 20
    c: Tangent(g4,g0) = 1.5708
    c: Horizontal(g5)
    c: Coincident(g6,g5)
    c: Coincident(g1,g6)
    c: Vertical(g6)
    c: Tangent(g5,g4) = -1.5708
    c: DistanceY(g6,g6) = 1
    c: DistanceX(g5,g0) = 56.5
    c: DistanceX(g0,g1) = 95
    c: DistanceX(g4,g0) = 22.5
FEATURE [PartDesign::Pocket] Pocket297  label="Swing Leg001"
  BaseFeature = -> Pocket302
  Length = 35
  Length2 = 100
  Profile = -> Sketch808
  Type = 0
FEATURE [PartDesign::Fillet] Fillet110  label="Servocable 001"
  Base = -> Pocket297 [Edge144,Edge135]
  BaseFeature = -> Pocket297
  Radius = 3
FEATURE [Sketcher::SketchObject] Sketch809
  ExternalGeometry = -> [Fillet110]
  MapMode = 5
  Placement = pos=(0,4.4e-15,20) rot=(0,0,1;0rad)
  Support = -> [Fillet110]
  sketch-geometry (12):
    g0: Circle CenterX=-82.3678 CenterY=12.6322 CenterZ=0 NormalX=0 NormalY=0 NormalZ=1 AngleXU=0 Radius=1.6
    g1: LineSegment [constr] StartX=-80 StartY=15 StartZ=0 EndX=-83.2345 EndY=15.8667 EndZ=0
    g2: LineSegment [constr] StartX=-83.2345 StartY=15.8667 StartZ=0 EndX=-85.6024 EndY=13.4988 EndZ=0
    g3: LineSegment [constr] StartX=-85.6024 StartY=13.4988 StartZ=0 EndX=-84.7357 EndY=10.2643 EndZ=0
    g4: LineSegment [constr] StartX=-84.7357 StartY=10.2643 StartZ=0 EndX=-81.5012 EndY=9.39763 EndZ=0
    g5: LineSegment [constr] StartX=-81.5012 StartY=9.39763 StartZ=0 EndX=-79.1333 EndY=11.7655 EndZ=0
    g6: LineSegment [constr] StartX=-79.1333 StartY=11.7655 StartZ=0 EndX=-80 EndY=15 EndZ=0
    g7: Circle [constr] CenterX=-82.3678 CenterY=12.6322 CenterZ=0 NormalX=0 NormalY=0 NormalZ=1 AngleXU=0 Radius=3.34863
    g8: Circle CenterX=4 CenterY=20 CenterZ=0 NormalX=0 NormalY=0 NormalZ=1 AngleXU=0 Radius=1.6
    g9: Circle CenterX=52.5 CenterY=20 CenterZ=0 NormalX=0 NormalY=0 NormalZ=1 AngleXU=0 Radius=1.6
    g10: Circle CenterX=52.5 CenterY=10 CenterZ=0 NormalX=0 NormalY=0 NormalZ=1 AngleXU=0 Radius=1.6
    g11: Circle CenterX=4 CenterY=10 CenterZ=0 NormalX=0 NormalY=0 NormalZ=1 AngleXU=0 Radius=1.6
  constraints (30):
    c: Radius(g0) = 1.6
    c: Coincident(g1,g2)
    c: Coincident(g2,g3)
    c: Coincident(g3,g4)
    c: Coincident(g4,g5)
    c: Coincident(g5,g6)
    c: Coincident(g6,g1)
    c: Equal(g1, g2-g6) x5
    c: PointOnObject(g1,g7)
    c: PointOnObject(g2,g7)
    c: PointOnObject(g3,g7)
    c: PointOnObject(g4,g7)
    c: PointOnObject(g5,g7)
    c: PointOnObject(g6,g7)
    c: Coincident(g7,g0)
    c: Distance(g4,g2) = 5.8
    c: Coincident(g1,g-3)
    c: Angle(g5) = 0.785398
    c: Horizontal(g8,g9)
    c: Horizontal(g11,g10)
    c: Vertical(g10,g9)
    c: Vertical(g8,g11)
    c: Equal(g11,g8)
    c: Equal(g8,g9)
    c: Equal(g9,g10)
    c: Equal(g8,g0)
    c: DistanceX(g11,g10) = 48.5
    c: DistanceY(g11,g8) = 10
    c: DistanceY(g-1,g11) = 10
    c: DistanceX(g-1,g11) = 4
FEATURE [PartDesign::Pocket] Pocket301  label="Screwhole001"
  BaseFeature = -> Fillet110
  Length = 20
  Length2 = 100
  Profile = -> Sketch809
  Type = 0
FEATURE [Sketcher::SketchObject] Sketch815
  MapMode = 5
  Placement = pos=(0,4.4e-15,20) rot=(0,0,1;0rad)
  Support = -> [Pocket301]
  sketch-geometry (5):
    g0: ArcOfCircle CenterX=-80 CenterY=15 CenterZ=0 NormalX=0 NormalY=0 NormalZ=1 AngleXU=0 Radius=12.5 StartAngle=2.35619 EndAngle=5.49779
    g1: LineSegment [constr] StartX=-88.8388 StartY=23.8388 StartZ=0 EndX=-71.1612 EndY=6.16117 EndZ=0
    g2: LineSegment StartX=-88.8388 StartY=23.8388 StartZ=0 EndX=-92.3744 EndY=27.3744 EndZ=0
    g3: LineSegment StartX=-71.1612 StartY=6.16117 StartZ=0 EndX=-67.6256 EndY=2.62563 EndZ=0
    g4: ArcOfCircle CenterX=-80 CenterY=15 CenterZ=0 NormalX=0 NormalY=0 NormalZ=1 AngleXU=0 Radius=17.5 StartAngle=2.35619 EndAngle=5.49779
  constraints (15):
    c: Radius(g0) = 12.5
    c: DistanceX(g0,g-1) = 80
    c: DistanceY(g-1,g0) = 15
    c: Coincident(g1,g0)
    c: Coincident(g1,g0)
    c: Angle(g1) = -0.785398
    c: PointOnObject(g0,g1)
    c: Coincident(g2,g0)
    c: Coincident(g3,g0)
    c: Coincident(g4,g0)
    c: Coincident(g4,g2)
    c: Coincident(g4,g3)
    c: Tangent(g2,g1)
    c: Tangent(g1,g3)
    c: Radius(g4) = 17.5
FEATURE [PartDesign::Pocket] Pocket291  label="Rubberfoot Pocket001"
  BaseFeature = -> Pocket301
  Length = 20
  Length2 = 100
  Profile = -> Sketch815
  Type = 0
FEATURE [Sketcher::SketchObject] Sketch816
  AttachmentOffset = pos=(0,0,-3) rot=(0,0,1;0rad)
  ExternalGeometry = -> [Pocket291]
  MapMode = 5
  Placement = pos=(0,3.7e-15,17) rot=(0,0,1;0rad)
  Support = -> [Pocket291]
  sketch-geometry (10):
    g0: LineSegment [constr] StartX=-80 StartY=15 StartZ=0 EndX=-83.2345 EndY=15.8667 EndZ=0
    g1: LineSegment StartX=-83.2345 StartY=15.8667 StartZ=0 EndX=-85.6024 EndY=13.4988 EndZ=0
    g2: LineSegment StartX=-85.6024 StartY=13.4988 StartZ=0 EndX=-84.7357 EndY=10.2643 EndZ=0
    g3: LineSegment StartX=-84.7357 StartY=10.2643 StartZ=0 EndX=-81.5012 EndY=9.39763 EndZ=0
    g4: LineSegment StartX=-81.5012 StartY=9.39763 StartZ=0 EndX=-79.1333 EndY=11.7655 EndZ=0
    g5: LineSegment [constr] StartX=-79.1333 StartY=11.7655 StartZ=0 EndX=-80 EndY=15 EndZ=0
    g6: Circle [constr] CenterX=-82.3678 CenterY=12.6322 CenterZ=0 NormalX=0 NormalY=0 NormalZ=1 AngleXU=0 Radius=3.34863
    g7: LineSegment StartX=-79.1333 StartY=11.7655 StartZ=0 EndX=-77.7191 EndY=13.1797 EndZ=0
    g8: LineSegment StartX=-77.7191 StartY=13.1797 StartZ=0 EndX=-81.8203 EndY=17.2809 EndZ=0
    g9: LineSegment StartX=-81.8203 StartY=17.2809 StartZ=0 EndX=-83.2345 EndY=15.8667 EndZ=0
  constraints (23):
    c: Coincident(g0,g1)
    c: Coincident(g1,g2)
    c: Coincident(g2,g3)
    c: Coincident(g3,g4)
    c: Coincident(g4,g5)
    c: Coincident(g5,g0)
    c: Equal(g0, g1-g5) x5
    c: PointOnObject(g0,g6)
    c: PointOnObject(g1,g6)
    c: PointOnObject(g2,g6)
    c: PointOnObject(g3,g6)
    c: PointOnObject(g4,g6)
    c: PointOnObject(g5,g6)
    c: Coincident(g6,g-3)
    c: Angle(g4) = 0.785398
    c: Distance(g1,g3) = 5.8
    c: Coincident(g8,g7)
    c: Coincident(g9,g8)
    c: Coincident(g9,g0)
    c: Tangent(g7,g4) = -1.5708
    c: Tangent(g9,g1)
    c: Perpendicular(g8,g7)
    c: Distance(g7) = 2
FEATURE [PartDesign::Pocket] Pocket310  label="Nuthole #003"
  BaseFeature = -> Pocket291
  Length = 3
  Length2 = 100
  Profile = -> Sketch816
  Type = 0
FEATURE [Sketcher::SketchObject] Sketch818
  AttachmentOffset = pos=(0,0,-17) rot=(0,0,1;0rad)
  ExternalGeometry = -> [Pocket291]
  MapMode = 5
  Placement = pos=(0,7e-16,3) rot=(0,0,1;0rad)
  Support = -> [Pocket291]
  sketch-geometry (10):
    g0: LineSegment [constr] StartX=-80 StartY=15 StartZ=0 EndX=-83.2345 EndY=15.8667 EndZ=0
    g1: LineSegment StartX=-83.2345 StartY=15.8667 StartZ=0 EndX=-85.6024 EndY=13.4988 EndZ=0
    g2: LineSegment StartX=-85.6024 StartY=13.4988 StartZ=0 EndX=-84.7357 EndY=10.2643 EndZ=0
    g3: LineSegment StartX=-84.7357 StartY=10.2643 StartZ=0 EndX=-81.5012 EndY=9.39763 EndZ=0
    g4: LineSegment StartX=-81.5012 StartY=9.39763 StartZ=0 EndX=-79.1333 EndY=11.7655 EndZ=0
    g5: LineSegment [constr] StartX=-79.1333 StartY=11.7655 StartZ=0 EndX=-80 EndY=15 EndZ=0
    g6: Circle [constr] CenterX=-82.3678 CenterY=12.6322 CenterZ=0 NormalX=0 NormalY=0 NormalZ=1 AngleXU=0 Radius=3.34863
    g7: LineSegment StartX=-79.1333 StartY=11.7655 StartZ=0 EndX=-77.7191 EndY=13.1797 EndZ=0
    g8: LineSegment StartX=-77.7191 StartY=13.1797 StartZ=0 EndX=-81.8203 EndY=17.2809 EndZ=0
    g9: LineSegment StartX=-81.8203 StartY=17.2809 StartZ=0 EndX=-83.2345 EndY=15.8667 EndZ=0
  constraints (23):
    c: Coincident(g0,g1)
    c: Coincident(g1,g2)
    c: Coincident(g2,g3)
    c: Coincident(g3,g4)
    c: Coincident(g4,g5)
    c: Coincident(g5,g0)
    c: Equal(g0, g1-g5) x5
    c: PointOnObject(g0,g6)
    c: PointOnObject(g1,g6)
    c: PointOnObject(g2,g6)
    c: PointOnObject(g3,g6)
    c: PointOnObject(g4,g6)
    c: PointOnObject(g5,g6)
    c: Coincident(g6,g-3)
    c: Angle(g4) = 0.785398
    c: Distance(g1,g3) = 5.8
    c: Coincident(g8,g7)
    c: Coincident(g9,g8)
    c: Coincident(g9,g0)
    c: Tangent(g7,g4) = -1.5708
    c: Tangent(g9,g1)
    c: Perpendicular(g8,g7)
    c: Distance(g7) = 2
FEATURE [PartDesign::Pocket] Pocket315  label="Nuthole #004"
  BaseFeature = -> Pocket310
  Length = 3
  Length2 = 100
  Profile = -> Sketch818
  Reversed = true
  Type = 0
FEATURE [PartDesign::Chamfer] Chamfer194  label="Smooth Nutholes001"
  Base = -> Pocket315 [Edge206,Edge207,Edge141,Edge209,Edge208,Edge225,Edge222,Edge223,Edge224,Edge221]
  BaseFeature = -> Pocket315
  Size = 0.625
FEATURE [Sketcher::SketchObject] Sketch797
  MapMode = 5
  Placement = pos=(0,0,10) rot=(0,0,1;0rad)
  Support = -> [Chamfer194]
  sketch-geometry (4):
    g0: LineSegment StartX=0 StartY=0 StartZ=0 EndX=56.5 EndY=0 EndZ=0
    g1: LineSegment StartX=56.5 StartY=0 StartZ=0 EndX=56.5 EndY=5 EndZ=0
    g2: LineSegment StartX=56.5 StartY=5 StartZ=0 EndX=0 EndY=5 EndZ=0
    g3: LineSegment StartX=0 StartY=5 StartZ=0 EndX=0 EndY=0 EndZ=0
  constraints (11):
    c: Coincident(g0,g1)
    c: Coincident(g1,g2)
    c: Coincident(g2,g3)
    c: Coincident(g3,g0)
    c: Horizontal(g0)
    c: Horizontal(g2)
    c: Vertical(g1)
    c: Vertical(g3)
    c: Coincident(g0,g-1)
    c: DistanceY(g1,g1) = 5
    c: DistanceX(g2,g2) = 56.5
FEATURE [PartDesign::Pocket] Pocket319  label="Shorten Baseplate001"
  BaseFeature = -> Chamfer194
  Length = 10
  Length2 = 100
  Profile = -> Sketch797
  Type = 0
FEATURE [PartDesign::Fillet] Fillet108  label="Smooth Corners001"
  Base = -> Pocket319 [Edge232,Edge234,Edge240,Edge242,Edge193,Edge83,Edge85,Edge86,Edge88,Edge170,Edge236,Edge238,Edge258]
  BaseFeature = -> Pocket319
  Radius = 0.4
FEATURE [PartDesign::Body] Body177  label="Wrist001"
  Group = -> [Sketch806,Pad311,Sketch810,Pocket320,Fillet111,Sketch799,Pocket306,Pad312,Sketch819,Pocket302,Sketch808,Pocket297,Fillet110,Sketch809,Pocket301,Sketch815,Pocket291,Sketch816,Sketch818,Pocket310,Pocket315,Chamfer194,Sketch797,Pocket319,Fillet108]
  Origin = -> Origin327
  Placement = pos=(-66.468,-10,83.4386) rot=(0.281085,0.678598,0.678598;3.68962rad)
  Tip = -> Fillet108
FEATURE [Sketcher::SketchObject] Sketch820
  MapMode = 5
  Support = -> [XY_Plane269]
  sketch-geometry (3):
    g0: Circle [constr] CenterX=0 CenterY=0 CenterZ=0 NormalX=0 NormalY=0 NormalZ=1 AngleXU=0 Radius=20
    g1: Circle CenterX=18.1039 CenterY=8.5 CenterZ=0 NormalX=0 NormalY=0 NormalZ=1 AngleXU=0 Radius=1.25
    g2: Circle CenterX=18.1039 CenterY=-8.5 CenterZ=0 NormalX=0 NormalY=0 NormalZ=1 AngleXU=0 Radius=1.25
  constraints (7):
    c: Coincident(g0,g-1)
    c: Radius(g0) = 20
    c: PointOnObject(g1,g0)
    c: Radius(g1) = 1.25
    c: DistanceY(g-1,g1) = 8.5
    c: Equal(g2,g1)
    c: Symmetric(g2,g1,g-1)
FEATURE [Sketcher::SketchObject] Sketch823
  MapMode = 5
  Support = -> [XY_Plane271]
  sketch-geometry (8):
    g0: LineSegment StartX=0 StartY=3.17543 StartZ=0 EndX=-2.75 EndY=1.58771 EndZ=0
    g1: LineSegment StartX=-2.75 StartY=1.58771 StartZ=0 EndX=-2.75 EndY=-1.58771 EndZ=0
    g2: LineSegment StartX=-2.75 StartY=-1.58771 StartZ=0 EndX=0 EndY=-3.17543 EndZ=0
    g3: LineSegment StartX=0 StartY=-3.17543 StartZ=0 EndX=2.75 EndY=-1.58771 EndZ=0
    g4: LineSegment StartX=2.75 StartY=-1.58771 StartZ=0 EndX=2.75 EndY=1.58771 EndZ=0
    g5: LineSegment StartX=2.75 StartY=1.58771 StartZ=0 EndX=0 EndY=3.17543 EndZ=0
    g6: Circle [constr] CenterX=0 CenterY=0 CenterZ=0 NormalX=0 NormalY=0 NormalZ=1 AngleXU=0 Radius=3.17543
    g7: Circle CenterX=0 CenterY=0 CenterZ=0 NormalX=0 NormalY=0 NormalZ=1 AngleXU=0 Radius=1.5
  constraints (18):
    c: Coincident(g0,g1)
    c: Coincident(g1,g2)
    c: Coincident(g2,g3)
    c: Coincident(g3,g4)
    c: Coincident(g4,g5)
    c: Coincident(g5,g0)
    c: Equal(g0, g1-g5) x5
    c: PointOnObject(g0,g6)
    c: PointOnObject(g1,g6)
    c: PointOnObject(g2,g6)
    c: PointOnObject(g3,g6)
    c: PointOnObject(g4,g6)
    c: PointOnObject(g5,g6)
    c: Coincident(g6,g-1)
    c: PointOnObject(g5,g-2)
    c: DistanceX(g0,g4) = 5.5
    c: Coincident(g7,g-1)
    c: Radius(g7) = 1.5
FEATURE [PartDesign::Pad] Pad318  label="M3 Nut Primitive061"
  Length = 1.2
  Length2 = 1.2
  Profile = -> Sketch823
  Type = 4
FEATURE [Sketcher::SketchObject] Sketch825
  MapMode = 5
  Placement = pos=(0,0,-6.9576e-12) rot=(1,0,0;3.14159rad)
  Support = -> [Pad315]
  sketch-geometry (4):
    g0: ArcOfCircle CenterX=0 CenterY=0 CenterZ=0 NormalX=0 NormalY=0 NormalZ=1 AngleXU=0 Radius=20 StartAngle=2.29353 EndAngle=3.98965
    g1: LineSegment StartX=-13.2288 StartY=15 StartZ=0 EndX=-23.2288 EndY=15 EndZ=0
    g2: LineSegment StartX=-23.2288 StartY=15 StartZ=0 EndX=-23.2288 EndY=-15 EndZ=0
    g3: LineSegment StartX=-23.2288 StartY=-15 StartZ=0 EndX=-13.2288 EndY=-15 EndZ=0
  constraints (12):
    c: Coincident(g0,g-1)
    c: Vertical(g0,g0)
    c: Coincident(g0,g1)
    c: Coincident(g1,g2)
    c: Vertical(g2)
    c: Coincident(g2,g3)
    c: Coincident(g3,g0)
    c: Horizontal(g3)
    c: Radius(g0) = 20
    c: DistanceX(g1,g1) = 10
    c: DistanceY(g2,g2) = 30
    c: Horizontal(g1)
FEATURE [PartDesign::Groove] Groove067  label="Halfspherical Shape001"
  Angle = 360
  Axis = (0,-1,7e-16)
  Base = (0,0,-6.9577e-12)
  BaseFeature = -> Pad315
  Placement = pos=(0,0,0) rot=(1,0,0;1.5708rad)
  Profile = -> Sketch825
  ReferenceAxis = -> Sketch825 [V_Axis]
  Reversed = true
FEATURE [PartDesign::SubtractivePipe] SubtractivePipe010  label="Horizontal Profile001"
  AuxilleryCurvelinear = true
  AuxillerySpineTangent = false
  BaseFeature = -> Groove067
  Binormal = (0,0,0)
  Mode = 0
  Placement = pos=(0,0,0) rot=(1,0,0;1.5708rad)
  Profile = -> Sketch814
  Spine = -> Groove067 [Edge2,Edge1]
  SpineTangent = false
  Transformation = 0
  Transition = 0
FEATURE [PartDesign::PolarPattern] PolarPattern001  label="Horizontal Profile Polar Pattern001"
  Angle = 180
  Axis = -> Sketch814 [N_Axis]
  BaseFeature = -> SubtractivePipe010
  Occurrences = 12
  Originals = -> [SubtractivePipe010]
  Placement = pos=(0,0,0) rot=(1,0,0;1.5708rad)
  Reversed = true
FEATURE [PartDesign::Groove] Groove064  label="Vertical Profiles001"
  Angle = 360
  Axis = (0,1,0)
  Base = (0,0,0)
  BaseFeature = -> PolarPattern001
  Placement = pos=(0,0,0) rot=(1,0,0;1.5708rad)
  Profile = -> Sketch820
  ReferenceAxis = -> Sketch820 [V_Axis]
FEATURE [Sketcher::SketchObject] Sketch827
  ExternalGeometry = -> [Pad318]
  MapMode = 5
  Placement = pos=(0,0,0) rot=(0.57735,0.57735,0.57735;2.0944rad)
  Support = -> [YZ_Plane280]
  sketch-geometry (6):
    g0: LineSegment StartX=-2.67543 StartY=1.2 StartZ=0 EndX=-3.67543 EndY=1.2 EndZ=0
    g1: LineSegment StartX=-3.67543 StartY=1.2 StartZ=0 EndX=-3.67543 EndY=-1.2 EndZ=0
    g2: LineSegment StartX=-3.67543 StartY=-1.2 StartZ=0 EndX=-2.67543 EndY=-1.2 EndZ=0
    g3: LineSegment StartX=-2.67543 StartY=-1.2 StartZ=0 EndX=-3.17543 EndY=-1 EndZ=0
    g4: LineSegment StartX=-3.17543 StartY=-1 StartZ=0 EndX=-3.17543 EndY=1 EndZ=0
    g5: LineSegment StartX=-3.17543 StartY=1 StartZ=0 EndX=-2.67543 EndY=1.2 EndZ=0
  constraints (15):
    c: Horizontal(g0)
    c: Coincident(g0,g1)
    c: Coincident(g1,g2)
    c: Coincident(g2,g3)
    c: Coincident(g3,g4)
    c: Coincident(g4,g5)
    c: Coincident(g5,g0)
    c: Symmetric(g4,g3,g-1)
    c: Symmetric(g0,g2,g-1)
    c: Symmetric(g1,g0,g-1)
    c: DistanceX(g0,g4) = 0.5
    c: DistanceY(g3,g4) = 2
    c: DistanceY(g1,g0) = 2.4
    c: PointOnObject(g3,g-3)
    c: DistanceX(g4,g0) = 0.5
FEATURE [PartDesign::Groove] Groove069  label="M3 Nut Smooth065"
  Angle = 360
  Axis = (-2e-16,3e-16,1)
  Base = (0,0,0)
  BaseFeature = -> Pad318
  Profile = -> Sketch827
  ReferenceAxis = -> Sketch827 [V_Axis]
  Reversed = true
FEATURE [PartDesign::Chamfer] Chamfer189  label="M3 Nut Smooth Hole078"
  Base = -> Groove069 [Edge24,Edge23]
  BaseFeature = -> Groove069
  Size = 0.2
FEATURE [PartDesign::Body] Body170  label="M3 Nut031"
  Group = -> [Sketch823,Pad318,Sketch827,Groove069,Chamfer189]
  Origin = -> Origin369
  Placement = pos=(0.75,-5.5,34.25) rot=(1,0,0;1.5708rad)
  Tip = -> Chamfer189
FEATURE [Sketcher::SketchObject] Sketch828
  MapMode = 5
  Placement = pos=(0,0,0) rot=(1,0,0;1.5708rad)
  Support = -> [XZ_Plane286]
  sketch-geometry (2):
    g0: ArcOfCircle CenterX=0 CenterY=0 CenterZ=0 NormalX=0 NormalY=0 NormalZ=1 AngleXU=0 Radius=12.75 StartAngle=0 EndAngle=3.14159
    g1: LineSegment StartX=-12.75 StartY=0 StartZ=0 EndX=12.75 EndY=0 EndZ=0
  constraints (6):
    c: Coincident(g0,g-1)
    c: Coincident(g1,g0)
    c: Coincident(g1,g0)
    c: Horizontal(g1)
    c: PointOnObject(g0,g1)
    c: Radius(g0) = 12.75
FEATURE [Sketcher::SketchObject] Sketch830
  MapMode = 5
  Placement = pos=(0,0,0) rot=(1,0,0;1.5708rad)
  Support = -> [XZ_Plane286]
  sketch-geometry (8):
    g0: LineSegment [constr] StartX=-4e-16 StartY=6.69726 StartZ=0 EndX=-2.9 EndY=5.02295 EndZ=0
    g1: LineSegment [constr] StartX=-2.9 StartY=5.02295 StartZ=0 EndX=-2.9 EndY=1.67432 EndZ=0
    g2: LineSegment [constr] StartX=-2.9 StartY=1.67432 StartZ=0 EndX=0 EndY=0 EndZ=0
    g3: LineSegment [constr] StartX=0 StartY=0 StartZ=0 EndX=2.9 EndY=1.67432 EndZ=0
    g4: LineSegment [constr] StartX=2.9 StartY=1.67432 StartZ=0 EndX=2.9 EndY=5.02295 EndZ=0
    g5: LineSegment [constr] StartX=2.9 StartY=5.02295 StartZ=0 EndX=-4e-16 EndY=6.69726 EndZ=0
    g6: Circle [constr] CenterX=0 CenterY=3.34863 CenterZ=0 NormalX=0 NormalY=0 NormalZ=1 AngleXU=0 Radius=3.34863
    g7: Circle CenterX=0 CenterY=3.34863 CenterZ=0 NormalX=0 NormalY=0 NormalZ=1 AngleXU=0 Radius=1.6
  constraints (18):
    c: Coincident(g0,g1)
    c: Coincident(g1,g2)
    c: Coincident(g2,g3)
    c: Coincident(g3,g4)
    c: Coincident(g4,g5)
    c: Coincident(g5,g0)
    c: Equal(g0, g1-g5) x5
    c: PointOnObject(g0,g6)
    c: PointOnObject(g1,g6)
    c: PointOnObject(g2,g6)
    c: PointOnObject(g3,g6)
    c: PointOnObject(g4,g6)
    c: PointOnObject(g5,g6)
    c: PointOnObject(g6,g-2)
    c: DistanceX(g0,g4) = 5.8
    c: Coincident(g2,g-1)
    c: Coincident(g7,g6)
    c: Radius(g7) = 1.6
FEATURE [Sketcher::SketchObject] Sketch832
  MapMode = 5
  Support = -> [XY_Plane285]
  sketch-geometry (8):
    g0: LineSegment StartX=0 StartY=3.17543 StartZ=0 EndX=-2.75 EndY=1.58771 EndZ=0
    g1: LineSegment StartX=-2.75 StartY=1.58771 StartZ=0 EndX=-2.75 EndY=-1.58771 EndZ=0
    g2: LineSegment StartX=-2.75 StartY=-1.58771 StartZ=0 EndX=0 EndY=-3.17543 EndZ=0
    g3: LineSegment StartX=0 StartY=-3.17543 StartZ=0 EndX=2.75 EndY=-1.58771 EndZ=0
    g4: LineSegment StartX=2.75 StartY=-1.58771 StartZ=0 EndX=2.75 EndY=1.58771 EndZ=0
    g5: LineSegment StartX=2.75 StartY=1.58771 StartZ=0 EndX=0 EndY=3.17543 EndZ=0
    g6: Circle [constr] CenterX=0 CenterY=0 CenterZ=0 NormalX=0 NormalY=0 NormalZ=1 AngleXU=0 Radius=3.17543
    g7: Circle CenterX=0 CenterY=0 CenterZ=0 NormalX=0 NormalY=0 NormalZ=1 AngleXU=0 Radius=1.5
  constraints (18):
    c: Coincident(g0,g1)
    c: Coincident(g1,g2)
    c: Coincident(g2,g3)
    c: Coincident(g3,g4)
    c: Coincident(g4,g5)
    c: Coincident(g5,g0)
    c: Equal(g0, g1-g5) x5
    c: PointOnObject(g0,g6)
    c: PointOnObject(g1,g6)
    c: PointOnObject(g2,g6)
    c: PointOnObject(g3,g6)
    c: PointOnObject(g4,g6)
    c: PointOnObject(g5,g6)
    c: Coincident(g6,g-1)
    c: PointOnObject(g5,g-2)
    c: DistanceX(g0,g4) = 5.5
    c: Coincident(g7,g-1)
    c: Radius(g7) = 1.5
FEATURE [PartDesign::Pad] Pad332  label="M3 Nut Primitive066"
  Length = 1.2
  Length2 = 1.2
  Profile = -> Sketch832
  Type = 4
FEATURE [Sketcher::SketchObject] Sketch829
  ExternalGeometry = -> [Pad332]
  MapMode = 5
  Placement = pos=(0,0,0) rot=(0.57735,0.57735,0.57735;2.0944rad)
  Support = -> [YZ_Plane277]
  sketch-geometry (6):
    g0: LineSegment StartX=-2.67543 StartY=1.2 StartZ=0 EndX=-3.67543 EndY=1.2 EndZ=0
    g1: LineSegment StartX=-3.67543 StartY=1.2 StartZ=0 EndX=-3.67543 EndY=-1.2 EndZ=0
    g2: LineSegment StartX=-3.67543 StartY=-1.2 StartZ=0 EndX=-2.67543 EndY=-1.2 EndZ=0
    g3: LineSegment StartX=-2.67543 StartY=-1.2 StartZ=0 EndX=-3.17543 EndY=-1 EndZ=0
    g4: LineSegment StartX=-3.17543 StartY=-1 StartZ=0 EndX=-3.17543 EndY=1 EndZ=0
    g5: LineSegment StartX=-3.17543 StartY=1 StartZ=0 EndX=-2.67543 EndY=1.2 EndZ=0
  constraints (15):
    c: Horizontal(g0)
    c: Coincident(g0,g1)
    c: Coincident(g1,g2)
    c: Coincident(g2,g3)
    c: Coincident(g3,g4)
    c: Coincident(g4,g5)
    c: Coincident(g5,g0)
    c: Symmetric(g4,g3,g-1)
    c: Symmetric(g0,g2,g-1)
    c: Symmetric(g1,g0,g-1)
    c: DistanceX(g0,g4) = 0.5
    c: DistanceY(g3,g4) = 2
    c: DistanceY(g1,g0) = 2.4
    c: PointOnObject(g3,g-3)
    c: DistanceX(g4,g0) = 0.5
FEATURE [PartDesign::Groove] Groove072  label="M3 Nut Smooth068"
  Angle = 360
  Axis = (-2e-16,3e-16,1)
  Base = (0,0,0)
  BaseFeature = -> Pad332
  Profile = -> Sketch829
  ReferenceAxis = -> Sketch829 [V_Axis]
  Reversed = true
FEATURE [PartDesign::Chamfer] Chamfer193  label="M3 Nut Smooth Hole080"
  Base = -> Groove072 [Edge24,Edge23]
  BaseFeature = -> Groove072
  Size = 0.2
FEATURE [PartDesign::Body] Body168  label="M3 Nut030"
  Group = -> [Sketch832,Pad332,Sketch829,Groove072,Chamfer193]
  Origin = -> Origin339
  Placement = pos=(0.75,5.5,34.25) rot=(1,0,0;1.5708rad)
  Tip = -> Chamfer193
FEATURE [App::Part] Part107  label="Nuts001"
  Group = -> [Body170,Body168]
  Origin = -> Origin375
FEATURE [Sketcher::SketchObject] Sketch833
  MapMode = 5
  Support = -> [XY_Plane276]
  sketch-geometry (1):
    g0: Circle CenterX=0 CenterY=0 CenterZ=0 NormalX=0 NormalY=0 NormalZ=1 AngleXU=0 Radius=1.9
  constraints (2):
    c: Coincident(g0,g-1)
    c: Radius(g0) = 1.9
FEATURE [PartDesign::Pad] Pad317  label="M3x8 Head040"
  Length = 2
  Length2 = 100
  Profile = -> Sketch833
  Type = 0
FEATURE [Sketcher::SketchObject] Sketch834
  MapMode = 5
  Placement = pos=(0,0,0) rot=(1,0,0;1.5708rad)
  Support = -> [XZ_Plane286]
  sketch-geometry (6):
    g0: LineSegment StartX=-15 StartY=0 StartZ=0 EndX=-25 EndY=7.5 EndZ=0
    g1: LineSegment StartX=-25 StartY=7.5 StartZ=0 EndX=-25 EndY=-7.5 EndZ=0
    g2: LineSegment StartX=-25 StartY=-7.5 StartZ=0 EndX=25 EndY=-7.5 EndZ=0
    g3: LineSegment StartX=25 StartY=-7.5 StartZ=0 EndX=25 EndY=7.5 EndZ=0
    g4: LineSegment StartX=25 StartY=7.5 StartZ=0 EndX=15 EndY=0 EndZ=0
    g5: LineSegment StartX=15 StartY=0 StartZ=0 EndX=-15 EndY=0 EndZ=0
  constraints (15):
    c: PointOnObject(g0,g-1)
    c: Coincident(g0,g1)
    c: Vertical(g1)
    c: Coincident(g1,g2)
    c: Horizontal(g2)
    c: Coincident(g2,g3)
    c: Coincident(g3,g4)
    c: Coincident(g4,g5)
    c: Coincident(g5,g0)
    c: DistanceX(g5,g5) = 30
    c: DistanceX(g4,g2) = 10
    c: Symmetric(g0,g4,g-2)
    c: Symmetric(g0,g3,g-2)
    c: DistanceY(g-1,g3) = 7.5
    c: Symmetric(g2,g3,g-1)
FEATURE [Sketcher::SketchObject] Sketch840
  MapMode = 5
  Placement = pos=(0,0,2) rot=(0,0,1;0rad)
  Support = -> [Pad317]
  sketch-geometry (1):
    g0: Circle CenterX=0 CenterY=0 CenterZ=0 NormalX=0 NormalY=0 NormalZ=1 AngleXU=0 Radius=1
  constraints (2):
    c: Coincident(g0,g-1)
    c: Radius(g0) = 1
FEATURE [PartDesign::Pad] Pad330  label="M3x8 Thread041"
  BaseFeature = -> Pad317
  Length = 8
  Length2 = 100
  Profile = -> Sketch840
  Type = 0
FEATURE [Sketcher::SketchObject] Sketch842
  MapMode = 5
  Support = -> [XY_Plane269]
  sketch-geometry (8):
    g0: LineSegment StartX=-20 StartY=14 StartZ=0 EndX=20 EndY=14 EndZ=0
    g1: LineSegment StartX=20 StartY=14 StartZ=0 EndX=20 EndY=19 EndZ=0
    g2: LineSegment StartX=20 StartY=19 StartZ=0 EndX=-20 EndY=19 EndZ=0
    g3: LineSegment StartX=-20 StartY=19 StartZ=0 EndX=-20 EndY=14 EndZ=0
    g4: LineSegment StartX=-20 StartY=-19 StartZ=0 EndX=20 EndY=-19 EndZ=0
    g5: LineSegment StartX=20 StartY=-19 StartZ=0 EndX=20 EndY=-14 EndZ=0
    g6: LineSegment StartX=20 StartY=-14 StartZ=0 EndX=-20 EndY=-14 EndZ=0
    g7: LineSegment StartX=-20 StartY=-14 StartZ=0 EndX=-20 EndY=-19 EndZ=0
  constraints (22):
    c: Coincident(g0,g1)
    c: Coincident(g1,g2)
    c: Coincident(g2,g3)
    c: Coincident(g3,g0)
    c: Horizontal(g0)
    c: Vertical(g1)
    c: Vertical(g3)
    c: Coincident(g4,g5)
    c: Coincident(g5,g6)
    c: Coincident(g6,g7)
    c: Coincident(g7,g4)
    c: Horizontal(g4)
    c: Horizontal(g6)
    c: Vertical(g5)
    c: Vertical(g7)
    c: Equal(g1,g5)
    c: Equal(g6,g2)
    c: Symmetric(g1,g2,g-2)
    c: Symmetric(g1,g4,g-1)
    c: DistanceY(g1,g1) = 5
    c: DistanceY(g5,g0) = 28
    c: DistanceX(g2,g2) = 40
FEATURE [PartDesign::Pocket] Pocket308  label="Cut Sides001"
  BaseFeature = -> Groove064
  Length = 25
  Length2 = 100
  Placement = pos=(0,0,0) rot=(1,0,0;1.5708rad)
  Profile = -> Sketch842
  Reversed = true
  Type = 0
FEATURE [PartDesign::Pocket] Pocket303  label="Inner Halfspherical Cutout001"
  BaseFeature = -> Pocket308
  Length = 10
  Length2 = 10
  Placement = pos=(0,0,0) rot=(1,0,0;1.5708rad)
  Profile = -> Sketch828
  Type = 4
FEATURE [PartDesign::Pocket] Pocket307  label="Slanted Edge001"
  BaseFeature = -> Pocket303
  Length = 15
  Length2 = 15
  Placement = pos=(0,0,0) rot=(1,0,0;1.5708rad)
  Profile = -> Sketch834
  Type = 4
FEATURE [PartDesign::Pocket] Pocket328  label="Screwholes002"
  BaseFeature = -> Pocket307
  Length = 15
  Length2 = 15
  Placement = pos=(0,0,0) rot=(1,0,0;1.5708rad)
  Profile = -> Sketch830
  Type = 4
FEATURE [Sketcher::SketchObject] Sketch811
  ExternalGeometry = -> [Pocket328]
  MapMode = 5
  Placement = pos=(0,14,-6.2e-15) rot=(-1,0,0;1.5708rad)
  Support = -> [Pocket328]
  sketch-geometry (1):
    g0: Circle CenterX=0 CenterY=-3.34863 CenterZ=0 NormalX=0 NormalY=0 NormalZ=1 AngleXU=0 Radius=2.85
  constraints (2):
    c: Coincident(g0,g-3)
    c: Radius(g0) = 2.85
FEATURE [PartDesign::Pocket] Pocket316  label="Screwhead Left001"
  BaseFeature = -> Pocket328
  Length = 2.5
  Length2 = 100
  Placement = pos=(0,0,0) rot=(1,0,0;1.5708rad)
  Profile = -> Sketch811
  Type = 0
FEATURE [Sketcher::SketchObject] Sketch822
  ExternalGeometry = -> [Pocket316]
  MapMode = 5
  Placement = pos=(0,-14,6.2e-15) rot=(1,0,0;1.5708rad)
  Support = -> [Pocket316]
  sketch-geometry (1):
    g0: Circle CenterX=0 CenterY=3.34863 CenterZ=0 NormalX=0 NormalY=0 NormalZ=1 AngleXU=0 Radius=2.85
  constraints (2):
    c: Coincident(g-3,g0)
    c: Radius(g0) = 2.85
FEATURE [PartDesign::Pocket] Pocket318  label="Screwhead Right001"
  BaseFeature = -> Pocket316
  Length = 2.5
  Length2 = 100
  Placement = pos=(0,0,0) rot=(1,0,0;1.5708rad)
  Profile = -> Sketch822
  Type = 0
FEATURE [PartDesign::Body] Body217  label="Foot_Tip001"
  Group = -> [Sketch813,Pad315,Sketch825,Groove067,Sketch814,SubtractivePipe010,PolarPattern001,Sketch820,Groove064,Sketch842,Pocket308,Sketch828,Pocket303,Sketch834,Pocket307,Sketch830,Pocket328,Sketch811,Pocket316,Sketch822,Pocket318]
  Origin = -> Origin366
  Placement = pos=(0.75,0,37.62) rot=(0,1,0;3.14159rad)
  Tip = -> Pocket318
FEATURE [App::Part] Part084  label="Lower Leg and foot001"
  Group = -> [Body177,Body217]
  Origin = -> Origin350
FEATURE [Sketcher::SketchObject] Sketch843
  MapMode = 5
  Support = -> [XY_Plane265]
  sketch-geometry (1):
    g0: Circle CenterX=0 CenterY=0 CenterZ=0 NormalX=0 NormalY=0 NormalZ=1 AngleXU=0 Radius=2.75
  constraints (2):
    c: Coincident(g0,g-1)
    c: Radius(g0) = 2.75
FEATURE [PartDesign::Pad] Pad327  label="M3x8 Head042"
  Length = 3
  Length2 = 100
  Profile = -> Sketch843
  Type = 0
FEATURE [Sketcher::SketchObject] Sketch831
  MapMode = 5
  Placement = pos=(0,0,3) rot=(0,0,1;0rad)
  Support = -> [Pad327]
  sketch-geometry (1):
    g0: Circle CenterX=0 CenterY=0 CenterZ=0 NormalX=0 NormalY=0 NormalZ=1 AngleXU=0 Radius=1.5
  constraints (2):
    c: Coincident(g0,g-1)
    c: Radius(g0) = 1.5
FEATURE [PartDesign::Pad] Pad339  label="M3x8 Thread042"
  BaseFeature = -> Pad327
  Length = 8
  Length2 = 100
  Profile = -> Sketch831
  Type = 0
FEATURE [Sketcher::SketchObject] Sketch824
  MapMode = 5
  Placement = pos=(0,0,0) rot=(1,0,0;3.14159rad)
  Support = -> [Pad339]
  sketch-geometry (7):
    g0: LineSegment StartX=1.275 StartY=0.736122 StartZ=0 EndX=0 EndY=1.47224 EndZ=0
    g1: LineSegment StartX=0 StartY=1.47224 StartZ=0 EndX=-1.275 EndY=0.736122 EndZ=0
    g2: LineSegment StartX=-1.275 StartY=0.736122 StartZ=0 EndX=-1.275 EndY=-0.736122 EndZ=0
    g3: LineSegment StartX=-1.275 StartY=-0.736122 StartZ=0 EndX=1.34766e-11 EndY=-1.47224 EndZ=0
    g4: LineSegment StartX=1.34766e-11 StartY=-1.47224 StartZ=0 EndX=1.275 EndY=-0.736122 EndZ=0
    g5: LineSegment StartX=1.275 StartY=-0.736122 StartZ=0 EndX=1.275 EndY=0.736122 EndZ=0
    g6: Circle [constr] CenterX=0 CenterY=0 CenterZ=0 NormalX=0 NormalY=0 NormalZ=1 AngleXU=0 Radius=1.47224
  constraints (16):
    c: Coincident(g0,g1)
    c: Coincident(g1,g2)
    c: Coincident(g2,g3)
    c: Coincident(g3,g4)
    c: Coincident(g4,g5)
    c: Coincident(g5,g0)
    c: Equal(g0, g1-g5) x5
    c: PointOnObject(g0,g6)
    c: PointOnObject(g1,g6)
    c: PointOnObject(g2,g6)
    c: PointOnObject(g3,g6)
    c: PointOnObject(g4,g6)
    c: PointOnObject(g5,g6)
    c: Coincident(g6,g-1)
    c: PointOnObject(g0,g-2)
    c: DistanceX(g1,g0) = 2.55
FEATURE [PartDesign::Pocket] Pocket325  label="M3x8 Wrench042"
  BaseFeature = -> Pad339
  Length = 1.3
  Length2 = 100
  Profile = -> Sketch824
  Type = 0
FEATURE [PartDesign::Chamfer] Chamfer190  label="M3x8 Smooth054"
  Base = -> Pocket325 [Face11,Edge2,Edge24,Edge3]
  BaseFeature = -> Pocket325
  Size = 0.2
FEATURE [PartDesign::Body] Body167  label="M3x040"
  Group = -> [Sketch843,Pad327,Sketch831,Pad339,Sketch824,Pocket325,Chamfer190]
  Origin = -> Origin343
  Placement = pos=(0.75,-14,34.25) rot=(-1,0,0;1.5708rad)
  Tip = -> Chamfer190
FEATURE [Sketcher::SketchObject] Sketch844
  MapMode = 5
  Support = -> [XY_Plane288]
  sketch-geometry (1):
    g0: Circle CenterX=0 CenterY=0 CenterZ=0 NormalX=0 NormalY=0 NormalZ=1 AngleXU=0 Radius=2.75
  constraints (2):
    c: Coincident(g0,g-1)
    c: Radius(g0) = 2.75
FEATURE [PartDesign::Pad] Pad328  label="M3x8 Head043"
  Length = 3
  Length2 = 100
  Profile = -> Sketch844
  Type = 0
FEATURE [Sketcher::SketchObject] Sketch821
  MapMode = 5
  Placement = pos=(0,0,3) rot=(0,0,1;0rad)
  Support = -> [Pad328]
  sketch-geometry (1):
    g0: Circle CenterX=0 CenterY=0 CenterZ=0 NormalX=0 NormalY=0 NormalZ=1 AngleXU=0 Radius=1.5
  constraints (2):
    c: Coincident(g0,g-1)
    c: Radius(g0) = 1.5
FEATURE [PartDesign::Pad] Pad340  label="M3x8 Thread043"
  BaseFeature = -> Pad328
  Length = 8
  Length2 = 100
  Profile = -> Sketch821
  Type = 0
FEATURE [Sketcher::SketchObject] Sketch826
  MapMode = 5
  Placement = pos=(0,0,0) rot=(1,0,0;3.14159rad)
  Support = -> [Pad340]
  sketch-geometry (7):
    g0: LineSegment StartX=1.275 StartY=0.736122 StartZ=0 EndX=0 EndY=1.47224 EndZ=0
    g1: LineSegment StartX=0 StartY=1.47224 StartZ=0 EndX=-1.275 EndY=0.736122 EndZ=0
    g2: LineSegment StartX=-1.275 StartY=0.736122 StartZ=0 EndX=-1.275 EndY=-0.736122 EndZ=0
    g3: LineSegment StartX=-1.275 StartY=-0.736122 StartZ=0 EndX=1.34766e-11 EndY=-1.47224 EndZ=0
    g4: LineSegment StartX=1.34766e-11 StartY=-1.47224 StartZ=0 EndX=1.275 EndY=-0.736122 EndZ=0
    g5: LineSegment StartX=1.275 StartY=-0.736122 StartZ=0 EndX=1.275 EndY=0.736122 EndZ=0
    g6: Circle [constr] CenterX=0 CenterY=0 CenterZ=0 NormalX=0 NormalY=0 NormalZ=1 AngleXU=0 Radius=1.47224
  constraints (16):
    c: Coincident(g0,g1)
    c: Coincident(g1,g2)
    c: Coincident(g2,g3)
    c: Coincident(g3,g4)
    c: Coincident(g4,g5)
    c: Coincident(g5,g0)
    c: Equal(g0, g1-g5) x5
    c: PointOnObject(g0,g6)
    c: PointOnObject(g1,g6)
    c: PointOnObject(g2,g6)
    c: PointOnObject(g3,g6)
    c: PointOnObject(g4,g6)
    c: PointOnObject(g5,g6)
    c: Coincident(g6,g-1)
    c: PointOnObject(g0,g-2)
    c: DistanceX(g1,g0) = 2.55
FEATURE [PartDesign::Pocket] Pocket326  label="M3x8 Wrench043"
  BaseFeature = -> Pad340
  Length = 1.3
  Length2 = 100
  Profile = -> Sketch826
  Type = 0
FEATURE [PartDesign::Chamfer] Chamfer191  label="M3x8 Smooth055"
  Base = -> Pocket326 [Face11,Edge2,Edge24,Edge3]
  BaseFeature = -> Pocket326
  Size = 0.2
FEATURE [PartDesign::Body] Body201  label="M3x045"
  Group = -> [Sketch844,Pad328,Sketch821,Pad340,Sketch826,Pocket326,Chamfer191]
  Origin = -> Origin371
  Placement = pos=(0.72,13.88,34.3) rot=(1,0,0;1.5708rad)
  Tip = -> Chamfer191
FEATURE [App::Part] Part105  label="Screws007"
  Group = -> [Body167,Body201]
  Origin = -> Origin338
FEATURE [Sketcher::SketchObject] Sketch845
  MapMode = 5
  Support = -> [XY_Plane286]
  sketch-geometry (4):
    g0: LineSegment StartX=0 StartY=0 StartZ=0 EndX=56.5 EndY=0 EndZ=0
    g1: LineSegment StartX=56.5 StartY=0 StartZ=0 EndX=56.5 EndY=-22 EndZ=0
    g2: LineSegment StartX=56.5 StartY=-22 StartZ=0 EndX=0 EndY=-22 EndZ=0
    g3: LineSegment StartX=0 StartY=-22 StartZ=0 EndX=0 EndY=0 EndZ=0
  constraints (11):
    c: Coincident(g0,g1)
    c: Coincident(g1,g2)
    c: Coincident(g2,g3)
    c: Coincident(g3,g0)
    c: Horizontal(g0)
    c: Horizontal(g2)
    c: Vertical(g1)
    c: Vertical(g3)
    c: Coincident(g0,g-1)
    c: DistanceX(g2,g2) = 56.5
    c: DistanceY(g3,g3) = 22
FEATURE [PartDesign::Pad] Pad329  label="Baseplate016"
  Length = 25
  Length2 = 100
  Profile = -> Sketch845
  Type = 0
FEATURE [Sketcher::SketchObject] Sketch846
  MapMode = 5
  Support = -> [XY_Plane290]
  sketch-geometry (8):
    g0: LineSegment StartX=0 StartY=3.17543 StartZ=0 EndX=-2.75 EndY=1.58771 EndZ=0
    g1: LineSegment StartX=-2.75 StartY=1.58771 StartZ=0 EndX=-2.75 EndY=-1.58771 EndZ=0
    g2: LineSegment StartX=-2.75 StartY=-1.58771 StartZ=0 EndX=0 EndY=-3.17543 EndZ=0
    g3: LineSegment StartX=0 StartY=-3.17543 StartZ=0 EndX=2.75 EndY=-1.58771 EndZ=0
    g4: LineSegment StartX=2.75 StartY=-1.58771 StartZ=0 EndX=2.75 EndY=1.58771 EndZ=0
    g5: LineSegment StartX=2.75 StartY=1.58771 StartZ=0 EndX=0 EndY=3.17543 EndZ=0
    g6: Circle [constr] CenterX=0 CenterY=0 CenterZ=0 NormalX=0 NormalY=0 NormalZ=1 AngleXU=0 Radius=3.17543
    g7: Circle CenterX=0 CenterY=0 CenterZ=0 NormalX=0 NormalY=0 NormalZ=1 AngleXU=0 Radius=1.5
  constraints (18):
    c: Coincident(g0,g1)
    c: Coincident(g1,g2)
    c: Coincident(g2,g3)
    c: Coincident(g3,g4)
    c: Coincident(g4,g5)
    c: Coincident(g5,g0)
    c: Equal(g0, g1-g5) x5
    c: PointOnObject(g0,g6)
    c: PointOnObject(g1,g6)
    c: PointOnObject(g2,g6)
    c: PointOnObject(g3,g6)
    c: PointOnObject(g4,g6)
    c: PointOnObject(g5,g6)
    c: Coincident(g6,g-1)
    c: PointOnObject(g5,g-2)
    c: DistanceX(g0,g4) = 5.5
    c: Coincident(g7,g-1)
    c: Radius(g7) = 1.5
FEATURE [PartDesign::Pad] Pad325  label="M3 Nut Primitive065"
  Length = 1.2
  Length2 = 1.2
  Profile = -> Sketch846
  Type = 4
FEATURE [Sketcher::SketchObject] Sketch847
  MapMode = 5
  Support = -> [XY_Plane280]
  sketch-geometry (8):
    g0: LineSegment StartX=0 StartY=3.17543 StartZ=0 EndX=-2.75 EndY=1.58771 EndZ=0
    g1: LineSegment StartX=-2.75 StartY=1.58771 StartZ=0 EndX=-2.75 EndY=-1.58771 EndZ=0
    g2: LineSegment StartX=-2.75 StartY=-1.58771 StartZ=0 EndX=0 EndY=-3.17543 EndZ=0
    g3: LineSegment StartX=0 StartY=-3.17543 StartZ=0 EndX=2.75 EndY=-1.58771 EndZ=0
    g4: LineSegment StartX=2.75 StartY=-1.58771 StartZ=0 EndX=2.75 EndY=1.58771 EndZ=0
    g5: LineSegment StartX=2.75 StartY=1.58771 StartZ=0 EndX=0 EndY=3.17543 EndZ=0
    g6: Circle [constr] CenterX=0 CenterY=0 CenterZ=0 NormalX=0 NormalY=0 NormalZ=1 AngleXU=0 Radius=3.17543
    g7: Circle CenterX=0 CenterY=0 CenterZ=0 NormalX=0 NormalY=0 NormalZ=1 AngleXU=0 Radius=1.5
  constraints (18):
    c: Coincident(g0,g1)
    c: Coincident(g1,g2)
    c: Coincident(g2,g3)
    c: Coincident(g3,g4)
    c: Coincident(g4,g5)
    c: Coincident(g5,g0)
    c: Equal(g0, g1-g5) x5
    c: PointOnObject(g0,g6)
    c: PointOnObject(g1,g6)
    c: PointOnObject(g2,g6)
    c: PointOnObject(g3,g6)
    c: PointOnObject(g4,g6)
    c: PointOnObject(g5,g6)
    c: Coincident(g6,g-1)
    c: PointOnObject(g5,g-2)
    c: DistanceX(g0,g4) = 5.5
    c: Coincident(g7,g-1)
    c: Radius(g7) = 1.5
FEATURE [PartDesign::Pad] Pad324  label="M3 Nut Primitive064"
  Length = 1.2
  Length2 = 1.2
  Profile = -> Sketch847
  Type = 4
FEATURE [Sketcher::SketchObject] Sketch849
  MapMode = 5
  Support = -> [XY_Plane284]
  sketch-geometry (8):
    g0: LineSegment StartX=0 StartY=2.3094 StartZ=0 EndX=-2 EndY=1.1547 EndZ=0
    g1: LineSegment StartX=-2 StartY=1.1547 StartZ=0 EndX=-2 EndY=-1.1547 EndZ=0
    g2: LineSegment StartX=-2 StartY=-1.1547 StartZ=0 EndX=-2e-16 EndY=-2.3094 EndZ=0
    g3: LineSegment StartX=-2e-16 StartY=-2.3094 StartZ=0 EndX=2 EndY=-1.1547 EndZ=0
    g4: LineSegment StartX=2 StartY=-1.1547 StartZ=0 EndX=2 EndY=1.1547 EndZ=0
    g5: LineSegment StartX=2 StartY=1.1547 StartZ=0 EndX=0 EndY=2.3094 EndZ=0
    g6: Circle [constr] CenterX=0 CenterY=0 CenterZ=0 NormalX=0 NormalY=0 NormalZ=1 AngleXU=0 Radius=2.3094
    g7: Circle CenterX=0 CenterY=0 CenterZ=0 NormalX=0 NormalY=0 NormalZ=1 AngleXU=0 Radius=1
  constraints (18):
    c: Coincident(g0,g1)
    c: Coincident(g1,g2)
    c: Coincident(g2,g3)
    c: Coincident(g3,g4)
    c: Coincident(g4,g5)
    c: Coincident(g5,g0)
    c: Equal(g0, g1-g5) x5
    c: PointOnObject(g0,g6)
    c: PointOnObject(g1,g6)
    c: PointOnObject(g2,g6)
    c: PointOnObject(g3,g6)
    c: PointOnObject(g4,g6)
    c: PointOnObject(g5,g6)
    c: Coincident(g6,g-1)
    c: PointOnObject(g5,g-2)
    c: DistanceX(g0,g4) = 4
    c: Coincident(g7,g-1)
    c: Radius(g7) = 1
FEATURE [PartDesign::Pad] Pad323  label="M3 Nut Primitive063"
  Length = 0.6
  Length2 = 0.6
  Profile = -> Sketch849
  Type = 4
FEATURE [Sketcher::SketchObject] Sketch836
  ExternalGeometry = -> [Pad323]
  MapMode = 5
  Placement = pos=(0,0,0) rot=(0.57735,0.57735,0.57735;2.0944rad)
  Support = -> [YZ_Plane284]
  sketch-geometry (6):
    g0: LineSegment StartX=-1.9594 StartY=0.6 StartZ=0 EndX=-2.8094 EndY=0.6 EndZ=0
    g1: LineSegment StartX=-2.8094 StartY=0.6 StartZ=0 EndX=-2.8094 EndY=-0.6 EndZ=0
    g2: LineSegment StartX=-2.8094 StartY=-0.6 StartZ=0 EndX=-1.9594 EndY=-0.6 EndZ=0
    g3: LineSegment StartX=-1.9594 StartY=-0.6 StartZ=0 EndX=-2.3094 EndY=-0.4 EndZ=0
    g4: LineSegment StartX=-2.3094 StartY=-0.4 StartZ=0 EndX=-2.3094 EndY=0.4 EndZ=0
    g5: LineSegment StartX=-2.3094 StartY=0.4 StartZ=0 EndX=-1.9594 EndY=0.6 EndZ=0
  constraints (15):
    c: Horizontal(g0)
    c: Coincident(g0,g1)
    c: Coincident(g1,g2)
    c: Coincident(g2,g3)
    c: Coincident(g3,g4)
    c: Coincident(g4,g5)
    c: Coincident(g5,g0)
    c: Symmetric(g4,g3,g-1)
    c: Symmetric(g0,g2,g-1)
    c: Symmetric(g1,g0,g-1)
    c: DistanceX(g0,g4) = 0.5
    c: DistanceY(g3,g4) = 0.8
    c: DistanceY(g1,g0) = 1.2
    c: PointOnObject(g3,g-3)
    c: DistanceX(g4,g0) = 0.35
FEATURE [PartDesign::Groove] Groove065  label="M3 Nut Smooth062"
  Angle = 360
  Axis = (-2e-16,3e-16,1)
  Base = (0,0,0)
  BaseFeature = -> Pad323
  Profile = -> Sketch836
  ReferenceAxis = -> Sketch836 [V_Axis]
  Reversed = true
FEATURE [PartDesign::Chamfer] Chamfer192  label="M3 Nut Smooth Hole079"
  Base = -> Groove065 [Edge24,Edge23]
  BaseFeature = -> Groove065
  Size = 0.2
FEATURE [PartDesign::Body] Body171  label="M2 Nut026"
  Group = -> [Sketch849,Pad323,Sketch836,Groove065,Chamfer192]
  Origin = -> Origin363
  Placement = pos=(-132.366,-135.25,71.5732) rot=(0.862856,0.357407,-0.357407;1.71777rad)
  Tip = -> Chamfer192
FEATURE [Sketcher::SketchObject] Sketch850
  MapMode = 5
  Placement = pos=(0,0,25) rot=(0,0,1;0rad)
  Support = -> [Pad329]
  sketch-geometry (4):
    g0: LineSegment StartX=8 StartY=0 StartZ=0 EndX=48.5 EndY=0 EndZ=0
    g1: LineSegment StartX=48.5 StartY=0 StartZ=0 EndX=48.5 EndY=-19 EndZ=0
    g2: LineSegment StartX=48.5 StartY=-19 StartZ=0 EndX=8 EndY=-19 EndZ=0
    g3: LineSegment StartX=8 StartY=-19 StartZ=0 EndX=8 EndY=0 EndZ=0
  constraints (12):
    c: Coincident(g0,g1)
    c: Coincident(g1,g2)
    c: Coincident(g2,g3)
    c: Coincident(g3,g0)
    c: Horizontal(g0)
    c: Horizontal(g2)
    c: Vertical(g1)
    c: Vertical(g3)
    c: PointOnObject(g0,g-1)
    c: DistanceY(g3,g3) = 19
    c: DistanceX(g0,g0) = 40.5
    c: DistanceX(g-1,g0) = 8
FEATURE [PartDesign::Pocket] Pocket324  label="Servopocket001"
  BaseFeature = -> Pad329
  Length = 20
  Length2 = 100
  Profile = -> Sketch850
  Type = 0
FEATURE [Sketcher::SketchObject] Sketch848
  MapMode = 5
  Placement = pos=(0,0,25) rot=(0,0,1;0rad)
  Support = -> [Pocket324]
  sketch-geometry (5):
    g0: ArcOfCircle CenterX=22.5 CenterY=23.1875 CenterZ=0 NormalX=0 NormalY=0 NormalZ=1 AngleXU=0 Radius=45.1875 StartAngle=4.19118 EndAngle=4.71239
    g1: LineSegment StartX=22.5 StartY=-22 StartZ=0 EndX=56.5 EndY=-22 EndZ=0
    g2: LineSegment StartX=56.5 StartY=-22 StartZ=0 EndX=56.5 EndY=-23 EndZ=0
    g3: LineSegment StartX=56.5 StartY=-23 StartZ=0 EndX=0 EndY=-23 EndZ=0
    g4: LineSegment StartX=0 StartY=-23 StartZ=0 EndX=0 EndY=-16 EndZ=0
  constraints (15):
    c: PointOnObject(g0,g-2)
    c: Horizontal(g1)
    c: Coincident(g2,g1)
    c: Vertical(g2)
    c: Coincident(g3,g2)
    c: Horizontal(g3)
    c: Coincident(g4,g3)
    c: Coincident(g4,g0)
    c: Vertical(g4)
    c: Tangent(g1,g0) = -1.5708
    c: DistanceX(g0,g0) = 22.5
    c: DistanceY(g4,g4) = 7
    c: DistanceY(g2,g2) = 1
    c: DistanceY(g0,g-1) = 16
    c: DistanceX(g3,g3) = 56.5
FEATURE [PartDesign::Pocket] Pocket313  label="Swing Counterpart001"
  BaseFeature = -> Pocket324
  Length = 25
  Length2 = 100
  Profile = -> Sketch848
  Type = 0
FEATURE [Sketcher::SketchObject] Sketch839
  MapMode = 5
  Placement = pos=(56.5,0,0) rot=(0.57735,0.57735,0.57735;2.0944rad)
  Support = -> [Pocket313]
  sketch-geometry (8):
    g0: LineSegment StartX=-6 StartY=22.9 StartZ=0 EndX=-3 EndY=22.9 EndZ=0
    g1: LineSegment StartX=-3 StartY=22.9 StartZ=0 EndX=-3 EndY=17.1 EndZ=0
    g2: LineSegment StartX=-3 StartY=17.1 StartZ=0 EndX=-6 EndY=17.1 EndZ=0
    g3: LineSegment StartX=-6 StartY=17.1 StartZ=0 EndX=-6 EndY=22.9 EndZ=0
    g4: LineSegment StartX=-6 StartY=12.9 StartZ=0 EndX=-3 EndY=12.9 EndZ=0
    g5: LineSegment StartX=-3 StartY=12.9 StartZ=0 EndX=-3 EndY=7.1 EndZ=0
    g6: LineSegment StartX=-3 StartY=7.1 StartZ=0 EndX=-6 EndY=7.1 EndZ=0
    g7: LineSegment StartX=-6 StartY=7.1 StartZ=0 EndX=-6 EndY=12.9 EndZ=0
  constraints (24):
    c: Coincident(g0,g1)
    c: Coincident(g1,g2)
    c: Coincident(g2,g3)
    c: Coincident(g3,g0)
    c: Horizontal(g0)
    c: Horizontal(g2)
    c: Vertical(g1)
    c: Vertical(g3)
    c: Coincident(g4,g5)
    c: Coincident(g5,g6)
    c: Coincident(g6,g7)
    c: Coincident(g7,g4)
    c: Horizontal(g4)
    c: Horizontal(g6)
    c: Vertical(g5)
    c: Vertical(g7)
    c: Equal(g1,g5)
    c: Equal(g4,g2)
    c: Vertical(g1,g4)
    c: DistanceX(g0,g0) = 3
    c: DistanceY(g1,g1) = 5.8
    c: DistanceY(g5,g1) = 10
    c: DistanceY(g-1,g5) = 7.1
    c: DistanceX(g5,g-1) = 3
FEATURE [PartDesign::Pocket] Pocket292  label="Nutholes001"
  BaseFeature = -> Pocket313
  Length = 56.5
  Length2 = 100
  Profile = -> Sketch839
  Type = 0
FEATURE [Sketcher::SketchObject] Sketch838
  MapMode = 5
  Placement = pos=(0,0,0) rot=(0,0.707107,0.707107;3.14159rad)
  Support = -> [Pocket292]
  sketch-geometry (4):
    g0: Circle CenterX=-52.5 CenterY=20 CenterZ=0 NormalX=0 NormalY=0 NormalZ=1 AngleXU=0 Radius=1.6
    g1: Circle CenterX=-52.5 CenterY=10 CenterZ=0 NormalX=0 NormalY=0 NormalZ=1 AngleXU=0 Radius=1.6
    g2: Circle CenterX=-4 CenterY=20 CenterZ=0 NormalX=0 NormalY=0 NormalZ=1 AngleXU=0 Radius=1.6
    g3: Circle CenterX=-4 CenterY=10 CenterZ=0 NormalX=0 NormalY=0 NormalZ=1 AngleXU=0 Radius=1.6
  constraints (12):
    c: Horizontal(g2,g0)
    c: Horizontal(g1,g3)
    c: Vertical(g3,g2)
    c: Vertical(g0,g1)
    c: Equal(g0,g1)
    c: Equal(g1,g2)
    c: Equal(g2,g3)
    c: Radius(g2) = 1.6
    c: DistanceX(g0,g2) = 48.5
    c: DistanceY(g3,g2) = 10
    c: DistanceY(g-1,g3) = 10
    c: DistanceX(g3,g-1) = 4
FEATURE [PartDesign::Pocket] Pocket333  label="Screwholes003"
  BaseFeature = -> Pocket292
  Length = 8.5
  Length2 = 100
  Profile = -> Sketch838
  Type = 0
FEATURE [Sketcher::SketchObject] Sketch837
  MapMode = 5
  Placement = pos=(56.5,0,0) rot=(0.57735,0.57735,0.57735;2.0944rad)
  Support = -> [Pocket333]
  sketch-geometry (4):
    g0: ArcOfCircle CenterX=-12 CenterY=11.5 CenterZ=0 NormalX=0 NormalY=0 NormalZ=1 AngleXU=0 Radius=2.5 StartAngle=3.14159 EndAngle=6.28319
    g1: LineSegment StartX=-14.5 StartY=11.5 StartZ=0 EndX=-14.5 EndY=25 EndZ=0
    g2: LineSegment StartX=-14.5 StartY=25 StartZ=0 EndX=-9.5 EndY=25 EndZ=0
    g3: LineSegment StartX=-9.5 StartY=25 StartZ=0 EndX=-9.5 EndY=11.5 EndZ=0
  constraints (13):
    c: Horizontal(g0,g0)
    c: Horizontal(g0,g0)
    c: Coincident(g1,g0)
    c: Vertical(g1)
    c: Coincident(g2,g1)
    c: Horizontal(g2)
    c: Coincident(g3,g2)
    c: Coincident(g3,g0)
    c: Vertical(g3)
    c: Radius(g0) = 2.5
    c: DistanceX(g0,g-1) = 12
    c: DistanceY(g-1,g0) = 11.5
    c: DistanceY(g-1,g2) = 25
FEATURE [PartDesign::Pocket] Pocket304  label="Servocable Pocket001"
  BaseFeature = -> Pocket333
  Length = 8
  Length2 = 100
  Profile = -> Sketch837
  Type = 0
FEATURE [PartDesign::Fillet] Fillet100  label="Servocable Smooth Edges001"
  Base = -> Pocket304 [Edge48,Edge43]
  BaseFeature = -> Pocket304
  Radius = 0.5
FEATURE [Sketcher::SketchObject] Sketch841
  MapMode = 5
  Placement = pos=(0,-22,0) rot=(1,0,0;1.5708rad)
  Support = -> [Fillet100]
  sketch-geometry (1):
    g0: Circle CenterX=38.25 CenterY=15 CenterZ=0 NormalX=0 NormalY=0 NormalZ=1 AngleXU=0 Radius=0.95
  constraints (3):
    c: DistanceY(g-1,g0) = 15
    c: DistanceX(g-1,g0) = 38.25
    c: Radius(g0) = 0.95
FEATURE [PartDesign::Pocket] Pocket309  label="Ball Bearing Pin Screwhole001"
  BaseFeature = -> Fillet100
  Length = 3
  Length2 = 100
  Profile = -> Sketch841
  Type = 0
FEATURE [Sketcher::SketchObject] Sketch851
  ExternalGeometry = -> [Pad324]
  MapMode = 5
  Placement = pos=(0,0,0) rot=(0.57735,0.57735,0.57735;2.0944rad)
  Support = -> [YZ_Plane289]
  sketch-geometry (6):
    g0: LineSegment StartX=-2.67543 StartY=1.2 StartZ=0 EndX=-3.67543 EndY=1.2 EndZ=0
    g1: LineSegment StartX=-3.67543 StartY=1.2 StartZ=0 EndX=-3.67543 EndY=-1.2 EndZ=0
    g2: LineSegment StartX=-3.67543 StartY=-1.2 StartZ=0 EndX=-2.67543 EndY=-1.2 EndZ=0
    g3: LineSegment StartX=-2.67543 StartY=-1.2 StartZ=0 EndX=-3.17543 EndY=-1 EndZ=0
    g4: LineSegment StartX=-3.17543 StartY=-1 StartZ=0 EndX=-3.17543 EndY=1 EndZ=0
    g5: LineSegment StartX=-3.17543 StartY=1 StartZ=0 EndX=-2.67543 EndY=1.2 EndZ=0
  constraints (15):
    c: Horizontal(g0)
    c: Coincident(g0,g1)
    c: Coincident(g1,g2)
    c: Coincident(g2,g3)
    c: Coincident(g3,g4)
    c: Coincident(g4,g5)
    c: Coincident(g5,g0)
    c: Symmetric(g4,g3,g-1)
    c: Symmetric(g0,g2,g-1)
    c: Symmetric(g1,g0,g-1)
    c: DistanceX(g0,g4) = 0.5
    c: DistanceY(g3,g4) = 2
    c: DistanceY(g1,g0) = 2.4
    c: PointOnObject(g3,g-3)
    c: DistanceX(g4,g0) = 0.5
FEATURE [PartDesign::Groove] Groove063  label="M3 Nut Smooth061"
  Angle = 360
  Axis = (-2e-16,3e-16,1)
  Base = (0,0,0)
  BaseFeature = -> Pad324
  Profile = -> Sketch851
  ReferenceAxis = -> Sketch851 [V_Axis]
  Reversed = true
FEATURE [PartDesign::Chamfer] Chamfer182  label="M3 Nut Smooth Hole076"
  Base = -> Groove063 [Edge24,Edge23]
  BaseFeature = -> Groove063
  Size = 0.2
FEATURE [PartDesign::Body] Body206  label="M3 Nut036"
  Group = -> [Sketch847,Pad324,Sketch851,Groove063,Chamfer182]
  Origin = -> Origin332
  Placement = pos=(-111.697,-150.5,43.8385) rot=(0.862856,-0.357407,0.357407;1.71777rad)
  Tip = -> Chamfer182
FEATURE [Sketcher::SketchObject] Sketch854
  MapMode = 5
  Placement = pos=(0,0,0) rot=(1,0,0;3.14159rad)
  Support = -> [Pad330]
  sketch-geometry (7):
    g0: LineSegment StartX=0.77 StartY=0.44456 StartZ=0 EndX=0 EndY=0.889119 EndZ=0
    g1: LineSegment StartX=0 StartY=0.889119 StartZ=0 EndX=-0.77 EndY=0.44456 EndZ=0
    g2: LineSegment StartX=-0.77 StartY=0.44456 StartZ=0 EndX=-0.77 EndY=-0.44456 EndZ=0
    g3: LineSegment StartX=-0.77 StartY=-0.44456 StartZ=0 EndX=3.85628e-11 EndY=-0.889119 EndZ=0
    g4: LineSegment StartX=3.85628e-11 StartY=-0.889119 StartZ=0 EndX=0.77 EndY=-0.44456 EndZ=0
    g5: LineSegment StartX=0.77 StartY=-0.44456 StartZ=0 EndX=0.77 EndY=0.44456 EndZ=0
    g6: Circle [constr] CenterX=0 CenterY=0 CenterZ=0 NormalX=0 NormalY=0 NormalZ=1 AngleXU=0 Radius=0.889119
  constraints (16):
    c: Coincident(g0,g1)
    c: Coincident(g1,g2)
    c: Coincident(g2,g3)
    c: Coincident(g3,g4)
    c: Coincident(g4,g5)
    c: Coincident(g5,g0)
    c: Equal(g0, g1-g5) x5
    c: PointOnObject(g0,g6)
    c: PointOnObject(g1,g6)
    c: PointOnObject(g2,g6)
    c: PointOnObject(g3,g6)
    c: PointOnObject(g4,g6)
    c: PointOnObject(g5,g6)
    c: Coincident(g6,g-1)
    c: PointOnObject(g0,g-2)
    c: DistanceX(g1,g0) = 1.54
FEATURE [PartDesign::Pocket] Pocket314  label="M3x8 Wrench041"
  BaseFeature = -> Pad330
  Length = 1
  Length2 = 100
  Profile = -> Sketch854
  Type = 0
FEATURE [PartDesign::Chamfer] Chamfer177  label="M3x8 Smooth052"
  Base = -> Pocket314 [Face11,Edge2,Edge24,Edge3]
  BaseFeature = -> Pocket314
  Size = 0.2
FEATURE [PartDesign::Body] Body213  label="M2x039"
  Group = -> [Sketch833,Pad317,Sketch840,Pad330,Sketch854,Pocket314,Chamfer177]
  Origin = -> Origin348
  Placement = pos=(-132.394,-126,71.585) rot=(1,0,0;1.5708rad)
  Tip = -> Chamfer177
FEATURE [Sketcher::SketchObject] Sketch855
  MapMode = 5
  Placement = pos=(0,0,0) rot=(0.57735,0.57735,0.57735;2.0944rad)
  Support = -> [YZ_Plane294]
  sketch-geometry (4):
    g0: LineSegment StartX=35.5 StartY=12.9 StartZ=0 EndX=38.5 EndY=12.9 EndZ=0
    g1: LineSegment StartX=38.5 StartY=12.9 StartZ=0 EndX=38.5 EndY=7.1 EndZ=0
    g2: LineSegment StartX=38.5 StartY=7.1 StartZ=0 EndX=35.5 EndY=7.1 EndZ=0
    g3: LineSegment StartX=35.5 StartY=7.1 StartZ=0 EndX=35.5 EndY=12.9 EndZ=0
  constraints (12):
    c: Coincident(g0,g1)
    c: Coincident(g1,g2)
    c: Coincident(g2,g3)
    c: Coincident(g3,g0)
    c: Horizontal(g0)
    c: Horizontal(g2)
    c: Vertical(g1)
    c: Vertical(g3)
    c: DistanceY(g-1,g1) = 7.1
    c: DistanceY(g3,g3) = 5.8
    c: DistanceX(g0,g0) = 3
    c: DistanceX(g-1,g1) = 38.5
FEATURE [Sketcher::SketchObject] Sketch856
  ExternalGeometry = -> [Pocket309]
  MapMode = 5
  Placement = pos=(0,-19,0) rot=(0,0.707107,0.707107;3.14159rad)
  Support = -> [Pocket309]
  sketch-geometry (7):
    g0: LineSegment StartX=-36.2 StartY=16.1836 StartZ=0 EndX=-38.25 EndY=17.3671 EndZ=0
    g1: LineSegment StartX=-38.25 StartY=17.3671 StartZ=0 EndX=-40.3 EndY=16.1836 EndZ=0
    g2: LineSegment StartX=-40.3 StartY=16.1836 StartZ=0 EndX=-40.3 EndY=13.8164 EndZ=0
    g3: LineSegment StartX=-40.3 StartY=13.8164 StartZ=0 EndX=-38.25 EndY=12.6329 EndZ=0
    g4: LineSegment StartX=-38.25 StartY=12.6329 StartZ=0 EndX=-36.2 EndY=13.8164 EndZ=0
    g5: LineSegment StartX=-36.2 StartY=13.8164 StartZ=0 EndX=-36.2 EndY=16.1836 EndZ=0
    g6: Circle [constr] CenterX=-38.25 CenterY=15 CenterZ=0 NormalX=0 NormalY=0 NormalZ=1 AngleXU=0 Radius=2.36714
  constraints (16):
    c: Coincident(g0,g1)
    c: Coincident(g1,g2)
    c: Coincident(g2,g3)
    c: Coincident(g3,g4)
    c: Coincident(g4,g5)
    c: Coincident(g5,g0)
    c: Equal(g0, g1-g5) x5
    c: PointOnObject(g0,g6)
    c: PointOnObject(g1,g6)
    c: PointOnObject(g2,g6)
    c: PointOnObject(g3,g6)
    c: PointOnObject(g4,g6)
    c: PointOnObject(g5,g6)
    c: Coincident(g6,g-3)
    c: Vertical(g5)
    c: DistanceX(g1,g0) = 4.1
FEATURE [PartDesign::Pocket] Pocket322  label="Ball Bearing Pin Nuthole001"
  BaseFeature = -> Pocket309
  Length = 1.5
  Length2 = 100
  Profile = -> Sketch856
  Type = 0
FEATURE [PartDesign::Fillet] Fillet099  label="Smooth Counterpart Corner001"
  Base = -> Pocket322 [Edge3]
  BaseFeature = -> Pocket322
  Radius = 5
FEATURE [PartDesign::Fillet] Fillet102  label="Smooth Servo Pocket001"
  Base = -> Fillet099 [Edge80,Edge77,Edge76,Edge79,Edge95]
  BaseFeature = -> Fillet099
  Radius = 1
FEATURE [Sketcher::SketchObject] Sketch835
  MapMode = 5
  Placement = pos=(0,0,0) rot=(0,0.707107,0.707107;3.14159rad)
  Support = -> [Fillet102]
  sketch-geometry (4):
    g0: LineSegment StartX=0 StartY=0 StartZ=0 EndX=-56.5 EndY=0 EndZ=0
    g1: LineSegment StartX=-56.5 StartY=0 StartZ=0 EndX=-56.5 EndY=5 EndZ=0
    g2: LineSegment StartX=-56.5 StartY=5 StartZ=0 EndX=0 EndY=5 EndZ=0
    g3: LineSegment StartX=0 StartY=5 StartZ=0 EndX=0 EndY=0 EndZ=0
  constraints (11):
    c: Coincident(g0,g1)
    c: Coincident(g1,g2)
    c: Coincident(g2,g3)
    c: Coincident(g3,g0)
    c: Horizontal(g0)
    c: Horizontal(g2)
    c: Vertical(g1)
    c: Vertical(g3)
    c: Coincident(g0,g-1)
    c: DistanceY(g1,g1) = 5
    c: DistanceX(g2,g2) = 56.5
FEATURE [PartDesign::Pad] Pad338  label="Elongate Baseplate001"
  BaseFeature = -> Fillet102
  Length = 10
  Length2 = 100
  Profile = -> Sketch835
  Type = 0
FEATURE [PartDesign::Fillet] Fillet112  label="Smooth Edges009"
  Base = -> Pad338 [Edge135,Edge159]
  BaseFeature = -> Pad338
  Radius = 0.4
FEATURE [PartDesign::Body] Body187  label="Wrist_Counterpart001"
  Group = -> [Sketch845,Pad329,Sketch850,Pocket324,Sketch848,Pocket313,Sketch839,Pocket292,Sketch838,Pocket333,Sketch837,Pocket304,Fillet100,Sketch841,Pocket309,Sketch856,Pocket322,Fillet099,Fillet102,Sketch835,Pad338,Fillet112]
  Origin = -> Origin328
  Placement = pos=(-115.966,-155,33.9411) rot=(0.382683,0,0.92388;3.14159rad)
  Tip = -> Fillet112
FEATURE [Sketcher::SketchObject] Sketch859
  MapMode = 5
  Support = -> [XY_Plane287]
  sketch-geometry (8):
    g0: LineSegment StartX=0 StartY=3.17543 StartZ=0 EndX=-2.75 EndY=1.58771 EndZ=0
    g1: LineSegment StartX=-2.75 StartY=1.58771 StartZ=0 EndX=-2.75 EndY=-1.58771 EndZ=0
    g2: LineSegment StartX=-2.75 StartY=-1.58771 StartZ=0 EndX=0 EndY=-3.17543 EndZ=0
    g3: LineSegment StartX=0 StartY=-3.17543 StartZ=0 EndX=2.75 EndY=-1.58771 EndZ=0
    g4: LineSegment StartX=2.75 StartY=-1.58771 StartZ=0 EndX=2.75 EndY=1.58771 EndZ=0
    g5: LineSegment StartX=2.75 StartY=1.58771 StartZ=0 EndX=0 EndY=3.17543 EndZ=0
    g6: Circle [constr] CenterX=0 CenterY=0 CenterZ=0 NormalX=0 NormalY=0 NormalZ=1 AngleXU=0 Radius=3.17543
    g7: Circle CenterX=0 CenterY=0 CenterZ=0 NormalX=0 NormalY=0 NormalZ=1 AngleXU=0 Radius=1.5
  constraints (18):
    c: Coincident(g0,g1)
    c: Coincident(g1,g2)
    c: Coincident(g2,g3)
    c: Coincident(g3,g4)
    c: Coincident(g4,g5)
    c: Coincident(g5,g0)
    c: Equal(g0, g1-g5) x5
    c: PointOnObject(g0,g6)
    c: PointOnObject(g1,g6)
    c: PointOnObject(g2,g6)
    c: PointOnObject(g3,g6)
    c: PointOnObject(g4,g6)
    c: PointOnObject(g5,g6)
    c: Coincident(g6,g-1)
    c: PointOnObject(g5,g-2)
    c: DistanceX(g0,g4) = 5.5
    c: Coincident(g7,g-1)
    c: Radius(g7) = 1.5
FEATURE [PartDesign::Pad] Pad336  label="M3 Nut Primitive067"
  Length = 1.2
  Length2 = 1.2
  Profile = -> Sketch859
  Type = 4
FEATURE [Sketcher::SketchObject] Sketch803
  ExternalGeometry = -> [Pad336]
  MapMode = 5
  Placement = pos=(0,0,0) rot=(0.57735,0.57735,0.57735;2.0944rad)
  Support = -> [YZ_Plane298]
  sketch-geometry (6):
    g0: LineSegment StartX=-2.67543 StartY=1.2 StartZ=0 EndX=-3.67543 EndY=1.2 EndZ=0
    g1: LineSegment StartX=-3.67543 StartY=1.2 StartZ=0 EndX=-3.67543 EndY=-1.2 EndZ=0
    g2: LineSegment StartX=-3.67543 StartY=-1.2 StartZ=0 EndX=-2.67543 EndY=-1.2 EndZ=0
    g3: LineSegment StartX=-2.67543 StartY=-1.2 StartZ=0 EndX=-3.17543 EndY=-1 EndZ=0
    g4: LineSegment StartX=-3.17543 StartY=-1 StartZ=0 EndX=-3.17543 EndY=1 EndZ=0
    g5: LineSegment StartX=-3.17543 StartY=1 StartZ=0 EndX=-2.67543 EndY=1.2 EndZ=0
  constraints (15):
    c: Horizontal(g0)
    c: Coincident(g0,g1)
    c: Coincident(g1,g2)
    c: Coincident(g2,g3)
    c: Coincident(g3,g4)
    c: Coincident(g4,g5)
    c: Coincident(g5,g0)
    c: Symmetric(g4,g3,g-1)
    c: Symmetric(g0,g2,g-1)
    c: Symmetric(g1,g0,g-1)
    c: DistanceX(g0,g4) = 0.5
    c: DistanceY(g3,g4) = 2
    c: DistanceY(g1,g0) = 2.4
    c: PointOnObject(g3,g-3)
    c: DistanceX(g4,g0) = 0.5
FEATURE [PartDesign::Groove] Groove071  label="M3 Nut Smooth067"
  Angle = 360
  Axis = (-2e-16,3e-16,1)
  Base = (0,0,0)
  BaseFeature = -> Pad336
  Profile = -> Sketch803
  ReferenceAxis = -> Sketch803 [V_Axis]
  Reversed = true
FEATURE [PartDesign::Chamfer] Chamfer179  label="M3 Nut Smooth Hole074"
  Base = -> Groove071 [Edge24,Edge23]
  BaseFeature = -> Groove071
  Size = 0.2
FEATURE [PartDesign::Body] Body221  label="M3 Nut038"
  Group = -> [Sketch859,Pad336,Sketch803,Groove071,Chamfer179]
  Origin = -> Origin358
  Placement = pos=(-146.027,-150.5,78.1297) rot=(0.862856,-0.357407,0.357407;1.71777rad)
  Tip = -> Chamfer179
FEATURE [Sketcher::SketchObject] Sketch860
  MapMode = 5
  Support = -> [XY_Plane289]
  sketch-geometry (12):
    g0: LineSegment StartX=0 StartY=0 StartZ=0 EndX=0 EndY=57 EndZ=0
    g1: LineSegment StartX=0 StartY=57 StartZ=0 EndX=40 EndY=57 EndZ=0
    g2: ArcOfCircle CenterX=40 CenterY=44.5 CenterZ=0 NormalX=0 NormalY=0 NormalZ=1 AngleXU=0 Radius=12.5 StartAngle=0.643501 EndAngle=1.5708
    g3: ArcOfCircle CenterX=60 CenterY=59.5 CenterZ=0 NormalX=0 NormalY=0 NormalZ=1 AngleXU=0 Radius=12.5 StartAngle=3.78509 EndAngle=4.71239
    g4: LineSegment StartX=60 StartY=47 StartZ=0 EndX=120 EndY=47 EndZ=0
    g5: ArcOfCircle CenterX=120 CenterY=37 CenterZ=0 NormalX=0 NormalY=0 NormalZ=1 AngleXU=0 Radius=10 StartAngle=2e-16 EndAngle=1.5708
    g6: LineSegment StartX=130 StartY=37 StartZ=0 EndX=130 EndY=15 EndZ=0
    g7: ArcOfCircle CenterX=125 CenterY=15 CenterZ=0 NormalX=0 NormalY=0 NormalZ=1 AngleXU=0 Radius=5 StartAngle=4.71239 EndAngle=6.28319
    g8: LineSegment StartX=125 StartY=10 StartZ=0 EndX=60 EndY=10 EndZ=0
    g9: LineSegment StartX=40 StartY=0 StartZ=0 EndX=0 EndY=0 EndZ=0
    g10: ArcOfCircle CenterX=40 CenterY=12.5 CenterZ=0 NormalX=0 NormalY=0 NormalZ=1 AngleXU=0 Radius=12.5 StartAngle=4.71239 EndAngle=5.63968
    g11: ArcOfCircle CenterX=60 CenterY=-2.5 CenterZ=0 NormalX=0 NormalY=0 NormalZ=1 AngleXU=0 Radius=12.5 StartAngle=1.5708 EndAngle=2.49809
  constraints (31):
    c: Coincident(g-1,g0)
    c: PointOnObject(g0,g-2)
    c: Coincident(g0,g1)
    c: Horizontal(g1)
    c: Tangent(g1,g2) = 1.5708
    c: Tangent(g2,g3) = 1.5708
    c: Tangent(g3,g4) = -1.5708
    c: Tangent(g4,g5) = 1.5708
    c: Tangent(g5,g6) = 1.5708
    c: Tangent(g6,g7) = 1.5708
    c: Tangent(g7,g8) = 1.5708
    c: Coincident(g9,g0)
    c: Horizontal(g9)
    c: Horizontal(g4)
    c: Horizontal(g8)
    c: Vertical(g6)
    c: Tangent(g11,g8) = -1.5708
    c: Tangent(g11,g10) = 1.5708
    c: Radius(g7) = 5
    c: Radius(g5) = 10
    c: DistanceX(g1,g1) = 40
    c: DistanceX(g0,g6) = 130
    c: DistanceX(g1,g3) = 20
    c: Tangent(g10,g9) = 1.5708
    c: DistanceX(g9,g8) = 20
    c: DistanceX(g9,g9) = 40
    c: DistanceY(g0,g0) = 57
    c: DistanceY(g9,g8) = 10
    c: DistanceY(g3,g1) = 10
    c: DistanceX(g10,g8) = 10
    c: DistanceX(g2,g3) = 10
FEATURE [PartDesign::Pad] Pad360  label="Baseplate018"
  Length = 30
  Length2 = 100
  Profile = -> Sketch860
  Type = 0
FEATURE [PartDesign::Pocket] Pocket346  label="Servohorn Mount Pocket003"
  BaseFeature = -> Pad360
  Length = 5
  Length2 = 100
  Profile = -> Pad360 [Face12]
  Type = 0
FEATURE [PartDesign::Pocket] Pocket352  label="Ball Bearing Mount Pocket002"
  BaseFeature = -> Pocket346
  Length = 5
  Length2 = 100
  Profile = -> Pocket346 [Face3]
  Type = 0
FEATURE [Sketcher::SketchObject] Sketch862
  ExternalGeometry = -> [Pad325]
  MapMode = 5
  Placement = pos=(0,0,0) rot=(0.57735,0.57735,0.57735;2.0944rad)
  Support = -> [YZ_Plane295]
  sketch-geometry (6):
    g0: LineSegment StartX=-2.67543 StartY=1.2 StartZ=0 EndX=-3.67543 EndY=1.2 EndZ=0
    g1: LineSegment StartX=-3.67543 StartY=1.2 StartZ=0 EndX=-3.67543 EndY=-1.2 EndZ=0
    g2: LineSegment StartX=-3.67543 StartY=-1.2 StartZ=0 EndX=-2.67543 EndY=-1.2 EndZ=0
    g3: LineSegment StartX=-2.67543 StartY=-1.2 StartZ=0 EndX=-3.17543 EndY=-1 EndZ=0
    g4: LineSegment StartX=-3.17543 StartY=-1 StartZ=0 EndX=-3.17543 EndY=1 EndZ=0
    g5: LineSegment StartX=-3.17543 StartY=1 StartZ=0 EndX=-2.67543 EndY=1.2 EndZ=0
  constraints (15):
    c: Horizontal(g0)
    c: Coincident(g0,g1)
    c: Coincident(g1,g2)
    c: Coincident(g2,g3)
    c: Coincident(g3,g4)
    c: Coincident(g4,g5)
    c: Coincident(g5,g0)
    c: Symmetric(g4,g3,g-1)
    c: Symmetric(g0,g2,g-1)
    c: Symmetric(g1,g0,g-1)
    c: DistanceX(g0,g4) = 0.5
    c: DistanceY(g3,g4) = 2
    c: DistanceY(g1,g0) = 2.4
    c: PointOnObject(g3,g-3)
    c: DistanceX(g4,g0) = 0.5
FEATURE [PartDesign::Groove] Groove068  label="M3 Nut Smooth064"
  Angle = 360
  Axis = (-2e-16,3e-16,1)
  Base = (0,0,0)
  BaseFeature = -> Pad325
  Profile = -> Sketch862
  ReferenceAxis = -> Sketch862 [V_Axis]
  Reversed = true
FEATURE [PartDesign::Chamfer] Chamfer184  label="M3 Nut Smooth Hole077"
  Base = -> Groove068 [Edge24,Edge23]
  BaseFeature = -> Groove068
  Size = 0.2
FEATURE [PartDesign::Body] Body204  label="M3 Nut035"
  Group = -> [Sketch846,Pad325,Sketch862,Groove068,Chamfer184]
  Origin = -> Origin345
  Placement = pos=(-104.661,-150.5,50.9359) rot=(0.862856,-0.357407,0.357407;1.71777rad)
  Tip = -> Chamfer184
FEATURE [Sketcher::SketchObject] Sketch864
  MapMode = 5
  Placement = pos=(0,0,0) rot=(0.57735,0.57735,0.57735;2.0944rad)
  Support = -> [YZ_Plane294]
  sketch-geometry (4):
    g0: LineSegment StartX=35.5 StartY=17.1 StartZ=0 EndX=38.5 EndY=17.1 EndZ=0
    g1: LineSegment StartX=38.5 StartY=17.1 StartZ=0 EndX=38.5 EndY=22.9 EndZ=0
    g2: LineSegment StartX=38.5 StartY=22.9 StartZ=0 EndX=35.5 EndY=22.9 EndZ=0
    g3: LineSegment StartX=35.5 StartY=22.9 StartZ=0 EndX=35.5 EndY=17.1 EndZ=0
  constraints (12):
    c: Coincident(g0,g1)
    c: Coincident(g1,g2)
    c: Coincident(g2,g3)
    c: Coincident(g3,g0)
    c: Horizontal(g0)
    c: Horizontal(g2)
    c: Vertical(g1)
    c: Vertical(g3)
    c: DistanceX(g2,g2) = 3
    c: DistanceY(g1,g1) = 5.8
    c: DistanceX(g-1,g0) = 38.5
    c: DistanceY(g-1,g0) = 17.1
FEATURE [Sketcher::SketchObject] Sketch868
  MapMode = 5
  Placement = pos=(0,0,0) rot=(1,0,0;1.5708rad)
  Support = -> [XZ_Plane293]
  sketch-geometry (4):
    g0: LineSegment StartX=68.5 StartY=25 StartZ=0 EndX=125 EndY=25 EndZ=0
    g1: LineSegment StartX=125 StartY=25 StartZ=0 EndX=125 EndY=5 EndZ=0
    g2: LineSegment StartX=125 StartY=5 StartZ=0 EndX=68.5 EndY=5 EndZ=0
    g3: LineSegment StartX=68.5 StartY=5 StartZ=0 EndX=68.5 EndY=25 EndZ=0
  constraints (12):
    c: Coincident(g0,g1)
    c: Coincident(g1,g2)
    c: Coincident(g2,g3)
    c: Coincident(g3,g0)
    c: Horizontal(g0)
    c: Horizontal(g2)
    c: Vertical(g1)
    c: Vertical(g3)
    c: DistanceX(g0,g0) = 56.5
    c: DistanceY(g3,g3) = 20
    c: DistanceY(g-1,g2) = 5
    c: DistanceX(g-1,g0) = 68.5
FEATURE [Sketcher::SketchObject] Sketch869
  MapMode = 5
  Support = -> [XY_Plane278]
  sketch-geometry (2):
    g0: Circle CenterX=0 CenterY=0 CenterZ=0 NormalX=0 NormalY=0 NormalZ=1 AngleXU=0 Radius=2.5
    g1: Circle CenterX=0 CenterY=0 CenterZ=0 NormalX=0 NormalY=0 NormalZ=1 AngleXU=0 Radius=1
  constraints (4):
    c: Coincident(g0,g-1)
    c: Coincident(g1,g0)
    c: Radius(g0) = 2.5
    c: Radius(g1) = 1
FEATURE [PartDesign::Pad] Pad322  label="Ball Bearing Pin002"
  Length = 5
  Length2 = 100
  Profile = -> Sketch869
  Type = 0
FEATURE [PartDesign::Chamfer] Chamfer188  label="Smooth Pinhead003"
  Base = -> Pad322 [Edge3]
  BaseFeature = -> Pad322
  Size = 0.4
FEATURE [PartDesign::Body] Body220  label="Shoulder_Joint_Ball_Bearing_Pin002"
  Group = -> [Sketch869,Pad322,Chamfer188]
  Origin = -> Origin325
  Placement = pos=(-132.396,-132.926,71.5546) rot=(-1,0,0;1.5708rad)
  Tip = -> Chamfer188
FEATURE [App::Part] Part085  label="Lower Leg Counterpiece and Ball Bearing Pin001"
  Group = -> [Body187,Body171,Body213,Body220,Body206,Body204,Body221,Body199]
  Origin = -> Origin373
  Placement = pos=(49.45,155,49.5) rot=(0,0,1;0rad)
FEATURE [Sketcher::SketchObject] Sketch874
  MapMode = 5
  Placement = pos=(40,0,0) rot=(0.57735,-0.57735,-0.57735;2.0944rad)
  Support = -> [Pocket352]
  sketch-geometry (6):
    g0: ArcOfCircle CenterX=-25.9999 CenterY=20 CenterZ=0 NormalX=0 NormalY=0 NormalZ=1 AngleXU=0 Radius=25.9999 StartAngle=6.28318 EndAngle=6.67798
    g1: LineSegment StartX=-2 StartY=30 StartZ=0 EndX=1 EndY=30 EndZ=0
    g2: LineSegment StartX=1 StartY=30 StartZ=0 EndX=1 EndY=0 EndZ=0
    g3: LineSegment StartX=1 StartY=0 StartZ=0 EndX=-2 EndY=2.39524e-11 EndZ=0
    g4: ArcOfCircle CenterX=-25.9999 CenterY=9.99999 CenterZ=0 NormalX=0 NormalY=0 NormalZ=1 AngleXU=0 Radius=25.9999 StartAngle=5.88839 EndAngle=6.28319
    g5: LineSegment StartX=-2.5011e-12 StartY=10 StartZ=0 EndX=-2.5011e-12 EndY=20 EndZ=0
  constraints (20):
    c: DistanceY(g0,g0) = 10
    c: DistanceX(g0,g-1) = 2
    c: Vertical(g0,g-1)
    c: Tangent(g0,g-2)
    c: DistanceY(g-1,g0) = 30
    c: Coincident(g0,g1)
    c: Coincident(g1,g2)
    c: PointOnObject(g2,g-1)
    c: Vertical(g2)
    c: Coincident(g2,g3)
    c: PointOnObject(g3,g-1)
    c: Coincident(g4,g3)
    c: Tangent(g4,g-2)
    c: Vertical(g3,g0)
    c: DistanceY(g-1,g4) = 10
    c: Coincident(g5,g4)
    c: Coincident(g5,g0)
    c: Vertical(g5)
    c: Horizontal(g1)
    c: DistanceX(g1,g1) = 3
FEATURE [PartDesign::SubtractivePipe] SubtractivePipe008  label="Smooth Beveled Surfaces002"
  AuxilleryCurvelinear = true
  AuxillerySpineTangent = false
  BaseFeature = -> Pocket352
  Binormal = (0,0,0)
  Mode = 0
  Profile = -> Sketch874
  Spine = -> Pocket352 [Edge21,Edge22,Edge23,Edge24,Edge25,Edge26,Edge27,Edge28,Edge29]
  SpineTangent = false
  Transformation = 0
  Transition = 0
FEATURE [PartDesign::Fillet] Fillet104  label="Smooth Edges008"
  Base = -> SubtractivePipe008 [Edge20,Edge5]
  BaseFeature = -> SubtractivePipe008
  Radius = 1.5
FEATURE [Sketcher::SketchObject] Sketch877
  MapMode = 5
  Support = -> [XY_Plane291]
  sketch-geometry (1):
    g0: Circle CenterX=0 CenterY=0 CenterZ=0 NormalX=0 NormalY=0 NormalZ=1 AngleXU=0 Radius=8
  constraints (2):
    c: Coincident(g0,g-1)
    c: Radius(g0) = 8
FEATURE [PartDesign::Pad] Pad366
  Length = 5
  Length2 = 100
  Profile = -> Sketch877
  Type = 0
FEATURE [Sketcher::SketchObject] Sketch879
  MapMode = 5
  Placement = pos=(0,0,0) rot=(1,0,0;1.5708rad)
  Support = -> [XZ_Plane294]
  sketch-geometry (4):
    g0: LineSegment StartX=68.5 StartY=25 StartZ=0 EndX=125 EndY=25 EndZ=0
    g1: LineSegment StartX=125 StartY=25 StartZ=0 EndX=125 EndY=5 EndZ=0
    g2: LineSegment StartX=125 StartY=5 StartZ=0 EndX=68.5 EndY=5 EndZ=0
    g3: LineSegment StartX=68.5 StartY=5 StartZ=0 EndX=68.5 EndY=25 EndZ=0
  constraints (12):
    c: Coincident(g0,g1)
    c: Coincident(g1,g2)
    c: Coincident(g2,g3)
    c: Coincident(g3,g0)
    c: Horizontal(g0)
    c: Horizontal(g2)
    c: Vertical(g1)
    c: Vertical(g3)
    c: DistanceX(g0,g0) = 56.5
    c: DistanceY(g3,g3) = 20
    c: DistanceY(g-1,g2) = 5
    c: DistanceX(g-1,g0) = 68.5
FEATURE [Sketcher::SketchObject] Sketch881
  MapMode = 5
  Support = -> [XY_Plane294]
  sketch-geometry (12):
    g0: LineSegment StartX=0 StartY=0 StartZ=0 EndX=0 EndY=57 EndZ=0
    g1: LineSegment StartX=0 StartY=57 StartZ=0 EndX=40 EndY=57 EndZ=0
    g2: ArcOfCircle CenterX=40 CenterY=44.5 CenterZ=0 NormalX=0 NormalY=0 NormalZ=1 AngleXU=0 Radius=12.5 StartAngle=0.643501 EndAngle=1.5708
    g3: ArcOfCircle CenterX=60 CenterY=59.5 CenterZ=0 NormalX=0 NormalY=0 NormalZ=1 AngleXU=0 Radius=12.5 StartAngle=3.78509 EndAngle=4.71239
    g4: LineSegment StartX=60 StartY=47 StartZ=0 EndX=120 EndY=47 EndZ=0
    g5: ArcOfCircle CenterX=120 CenterY=37 CenterZ=0 NormalX=0 NormalY=0 NormalZ=1 AngleXU=0 Radius=10 StartAngle=2e-16 EndAngle=1.5708
    g6: LineSegment StartX=130 StartY=37 StartZ=0 EndX=130 EndY=15 EndZ=0
    g7: ArcOfCircle CenterX=125 CenterY=15 CenterZ=0 NormalX=0 NormalY=0 NormalZ=1 AngleXU=0 Radius=5 StartAngle=4.71239 EndAngle=6.28319
    g8: LineSegment StartX=125 StartY=10 StartZ=0 EndX=60 EndY=10 EndZ=0
    g9: LineSegment StartX=40 StartY=0 StartZ=0 EndX=0 EndY=0 EndZ=0
    g10: ArcOfCircle CenterX=40 CenterY=12.5 CenterZ=0 NormalX=0 NormalY=0 NormalZ=1 AngleXU=0 Radius=12.5 StartAngle=4.71239 EndAngle=5.63968
    g11: ArcOfCircle CenterX=60 CenterY=-2.5 CenterZ=0 NormalX=0 NormalY=0 NormalZ=1 AngleXU=0 Radius=12.5 StartAngle=1.5708 EndAngle=2.49809
  constraints (31):
    c: Coincident(g-1,g0)
    c: PointOnObject(g0,g-2)
    c: Coincident(g0,g1)
    c: Horizontal(g1)
    c: Tangent(g1,g2) = 1.5708
    c: Tangent(g2,g3) = 1.5708
    c: Tangent(g3,g4) = -1.5708
    c: Tangent(g4,g5) = 1.5708
    c: Tangent(g5,g6) = 1.5708
    c: Tangent(g6,g7) = 1.5708
    c: Tangent(g7,g8) = 1.5708
    c: Coincident(g9,g0)
    c: Horizontal(g9)
    c: Horizontal(g4)
    c: Horizontal(g8)
    c: Vertical(g6)
    c: Tangent(g11,g8) = -1.5708
    c: Tangent(g11,g10) = 1.5708
    c: Radius(g7) = 5
    c: Radius(g5) = 10
    c: DistanceX(g1,g1) = 40
    c: DistanceX(g0,g6) = 130
    c: DistanceX(g1,g3) = 20
    c: Tangent(g10,g9) = 1.5708
    c: DistanceX(g9,g8) = 20
    c: DistanceX(g9,g9) = 40
    c: DistanceY(g0,g0) = 57
    c: DistanceY(g9,g8) = 10
    c: DistanceY(g3,g1) = 10
    c: DistanceX(g10,g8) = 10
    c: DistanceX(g2,g3) = 10
FEATURE [PartDesign::Pad] Pad358  label="Baseplate017"
  Length = 30
  Length2 = 100
  Profile = -> Sketch881
  Type = 0
FEATURE [PartDesign::Pocket] Pocket343  label="Servohorn Mount Pocket002"
  BaseFeature = -> Pad358
  Length = 5
  Length2 = 100
  Profile = -> Pad358 [Face12]
  Type = 0
FEATURE [PartDesign::Pocket] Pocket358  label="Ball Bearing Mount Pocket003"
  BaseFeature = -> Pocket343
  Length = 5
  Length2 = 100
  Profile = -> Pocket343 [Face3]
  Type = 0
FEATURE [Sketcher::SketchObject] Sketch876
  MapMode = 5
  Placement = pos=(40,0,0) rot=(0.57735,-0.57735,-0.57735;2.0944rad)
  Support = -> [Pocket358]
  sketch-geometry (6):
    g0: ArcOfCircle CenterX=-25.9999 CenterY=20 CenterZ=0 NormalX=0 NormalY=0 NormalZ=1 AngleXU=0 Radius=25.9999 StartAngle=6.28318 EndAngle=6.67798
    g1: LineSegment StartX=-2 StartY=30 StartZ=0 EndX=1 EndY=30 EndZ=0
    g2: LineSegment StartX=1 StartY=30 StartZ=0 EndX=1 EndY=0 EndZ=0
    g3: LineSegment StartX=1 StartY=0 StartZ=0 EndX=-2 EndY=2.39524e-11 EndZ=0
    g4: ArcOfCircle CenterX=-25.9999 CenterY=9.99999 CenterZ=0 NormalX=0 NormalY=0 NormalZ=1 AngleXU=0 Radius=25.9999 StartAngle=5.88839 EndAngle=6.28319
    g5: LineSegment StartX=-2.5011e-12 StartY=10 StartZ=0 EndX=-2.5011e-12 EndY=20 EndZ=0
  constraints (20):
    c: DistanceY(g0,g0) = 10
    c: DistanceX(g0,g-1) = 2
    c: Vertical(g0,g-1)
    c: Tangent(g0,g-2)
    c: DistanceY(g-1,g0) = 30
    c: Coincident(g0,g1)
    c: Coincident(g1,g2)
    c: PointOnObject(g2,g-1)
    c: Vertical(g2)
    c: Coincident(g2,g3)
    c: PointOnObject(g3,g-1)
    c: Coincident(g4,g3)
    c: Tangent(g4,g-2)
    c: Vertical(g3,g0)
    c: DistanceY(g-1,g4) = 10
    c: Coincident(g5,g4)
    c: Coincident(g5,g0)
    c: Vertical(g5)
    c: Horizontal(g1)
    c: DistanceX(g1,g1) = 3
FEATURE [PartDesign::SubtractivePipe] SubtractivePipe009  label="Smooth Beveled Surfaces003"
  AuxilleryCurvelinear = true
  AuxillerySpineTangent = false
  BaseFeature = -> Pocket358
  Binormal = (0,0,0)
  Mode = 0
  Profile = -> Sketch876
  Spine = -> Pocket358 [Edge21,Edge22,Edge23,Edge24,Edge25,Edge26,Edge27,Edge28,Edge29]
  SpineTangent = false
  Transformation = 0
  Transition = 0
FEATURE [Sketcher::SketchObject] Sketch882
  MapMode = 5
  Placement = pos=(0,5,0) rot=(1,0,0;1.5708rad)
  Support = -> [Fillet104]
  sketch-geometry (1):
    g0: Circle CenterX=0 CenterY=0 CenterZ=0 NormalX=0 NormalY=0 NormalZ=1 AngleXU=0 Radius=30
  constraints (2):
    c: Coincident(g0,g-1)
    c: Radius(g0) = 30
FEATURE [PartDesign::Pocket] Pocket353  label="Joint Pan003"
  BaseFeature = -> Fillet104
  Length = 47
  Length2 = 100
  Profile = -> Sketch882
  Type = 0
FEATURE [Sketcher::SketchObject] Sketch857
  ExternalGeometry = -> [Pocket353]
  MapMode = 5
  Placement = pos=(0,5,0) rot=(1,0,0;1.5708rad)
  Support = -> [Pocket353]
  sketch-geometry (7):
    g0: ArcOfCircle CenterX=23.5 CenterY=28.2018 CenterZ=0 NormalX=0 NormalY=0 NormalZ=1 AngleXU=0 Radius=1.79818 StartAngle=1.57079 EndAngle=2.66896
    g1: LineSegment StartX=21.8989 StartY=29.0204 StartZ=0 EndX=19.5977 EndY=24.5195 EndZ=0
    g2: ArcOfCircle CenterX=21.1988 CenterY=23.701 CenterZ=0 NormalX=0 NormalY=0 NormalZ=1 AngleXU=0 Radius=1.79818 StartAngle=2.66896 EndAngle=3.98266
    g3: Circle [constr] CenterX=0 CenterY=0 CenterZ=0 NormalX=0 NormalY=0 NormalZ=1 AngleXU=0 Radius=30
    g4: LineSegment StartX=23.5 StartY=30 StartZ=0 EndX=0 EndY=30 EndZ=0
    g5: LineSegment StartX=0 StartY=30 StartZ=0 EndX=0 EndY=22.3607 EndZ=0
    g6: LineSegment StartX=0 StartY=22.3607 StartZ=0 EndX=20 EndY=22.3607 EndZ=0
  constraints (19):
    c: Coincident(g3,g-1)
    c: Radius(g3) = 30
    c: Coincident(g4,g0)
    c: PointOnObject(g4,g3)
    c: Horizontal(g4)
    c: Tangent(g4,g0)
    c: Coincident(g5,g4)
    c: Vertical(g5)
    c: Tangent(g2,g3) = 1.5708
    c: Tangent(g2,g1) = -1.5708
    c: Tangent(g1,g0) = -1.5708
    c: DistanceX(g4,g4) = 23.5
    c: PointOnObject(g4,g-2)
    c: DistanceX(g5,g2) = 20
    c: Equal(g0,g2)
    c: Coincident(g6,g5)
    c: Coincident(g6,g2)
    c: Horizontal(g6)
    c: Horizontal(g-3,g0)
FEATURE [PartDesign::Pocket] Pocket344  label="Shortened Angled Top002"
  BaseFeature = -> Pocket353
  Length = 47
  Length2 = 100
  Profile = -> Sketch857
  Type = 0
FEATURE [PartDesign::Pocket] Pocket341  label="Servoplacement Helper Pocket002"
  BaseFeature = -> Pocket344
  Length = 15
  Length2 = 100
  Profile = -> Sketch879
  Type = 0
FEATURE [PartDesign::Pad] Pad361  label="Servoplacement Helper Pad003"
  BaseFeature = -> Pocket341
  Length = 5
  Length2 = 100
  Profile = -> Pocket341 [Face60]
  Type = 0
FEATURE [PartDesign::Fillet] Fillet105  label="Servoplacement Smooth Edges002"
  Base = -> Pad361 [Edge121,Edge125]
  BaseFeature = -> Pad361
  Radius = 0.4
FEATURE [Sketcher::SketchObject] Sketch873
  MapMode = 5
  Placement = pos=(0,10,-2.2e-15) rot=(1,0,0;1.5708rad)
  Support = -> [Fillet105]
  sketch-geometry (4):
    g0: LineSegment StartX=76.5 StartY=25 StartZ=0 EndX=117 EndY=25 EndZ=0
    g1: LineSegment StartX=117 StartY=25 StartZ=0 EndX=117 EndY=5 EndZ=0
    g2: LineSegment StartX=117 StartY=5 StartZ=0 EndX=76.5 EndY=5 EndZ=0
    g3: LineSegment StartX=76.5 StartY=5 StartZ=0 EndX=76.5 EndY=25 EndZ=0
  constraints (12):
    c: Coincident(g0,g1)
    c: Coincident(g1,g2)
    c: Coincident(g2,g3)
    c: Coincident(g3,g0)
    c: Horizontal(g0)
    c: Horizontal(g2)
    c: Vertical(g1)
    c: Vertical(g3)
    c: DistanceX(g0,g0) = 40.5
    c: DistanceY(g3,g3) = 20
    c: DistanceY(g-1,g2) = 5
    c: DistanceX(g-1,g2) = 76.5
FEATURE [PartDesign::Pocket] Pocket342  label="Servo Pocket005"
  BaseFeature = -> Fillet105
  Length = 30
  Length2 = 100
  Profile = -> Sketch873
  Type = 0
FEATURE [PartDesign::Fillet] Fillet106  label="Smooth Mount Edges002"
  Base = -> Pocket342 [Edge147,Edge146,Edge141,Edge152]
  BaseFeature = -> Pocket342
  Radius = 0.4
FEATURE [Sketcher::SketchObject] Sketch865
  MapMode = 5
  Placement = pos=(0,0,30) rot=(0,0,1;0rad)
  Support = -> [Fillet106]
  sketch-geometry (4):
    g0: LineSegment StartX=0 StartY=0 StartZ=0 EndX=130 EndY=0 EndZ=0
    g1: LineSegment StartX=130 StartY=0 StartZ=0 EndX=130 EndY=57 EndZ=0
    g2: LineSegment StartX=130 StartY=57 StartZ=0 EndX=0 EndY=57 EndZ=0
    g3: LineSegment StartX=0 StartY=57 StartZ=0 EndX=0 EndY=0 EndZ=0
  constraints (11):
    c: Coincident(g0,g1)
    c: Coincident(g1,g2)
    c: Coincident(g2,g3)
    c: Coincident(g3,g0)
    c: Horizontal(g0)
    c: Horizontal(g2)
    c: Vertical(g1)
    c: Vertical(g3)
    c: Coincident(g0,g-1)
    c: DistanceY(g1,g1) = 57
    c: DistanceX(g2,g2) = 130
FEATURE [PartDesign::Pocket] Pocket349  label="Remove Top Surface001"
  BaseFeature = -> Fillet106
  Length = 5
  Length2 = 100
  Profile = -> Sketch865
  Type = 0
FEATURE [Sketcher::SketchObject] Sketch861
  MapMode = 5
  Placement = pos=(0,0,25) rot=(0,0,1;0rad)
  Support = -> [Pocket349]
  sketch-geometry (7):
    g0: LineSegment StartX=0 StartY=43 StartZ=0 EndX=120 EndY=43 EndZ=0
    g1: ArcOfCircle CenterX=120 CenterY=38 CenterZ=0 NormalX=0 NormalY=0 NormalZ=1 AngleXU=0 Radius=5 StartAngle=3e-16 EndAngle=1.5708
    g2: LineSegment StartX=125 StartY=38 StartZ=0 EndX=125 EndY=10 EndZ=0
    g3: LineSegment StartX=125 StartY=10 StartZ=0 EndX=130 EndY=10 EndZ=0
    g4: LineSegment StartX=130 StartY=10 StartZ=0 EndX=130 EndY=57 EndZ=0
    g5: LineSegment StartX=130 StartY=57 StartZ=0 EndX=0 EndY=57 EndZ=0
    g6: LineSegment StartX=0 StartY=57 StartZ=0 EndX=0 EndY=43 EndZ=0
  constraints (20):
    c: Horizontal(g0)
    c: Tangent(g0,g1) = 1.5708
    c: Tangent(g1,g2) = 1.5708
    c: Coincident(g2,g3)
    c: Horizontal(g3)
    c: Coincident(g3,g4)
    c: Coincident(g4,g5)
    c: Horizontal(g5)
    c: Coincident(g5,g6)
    c: Coincident(g6,g0)
    c: Vertical(g6)
    c: Vertical(g4)
    c: Vertical(g2)
    c: PointOnObject(g0,g-2)
    c: DistanceY(g-1,g5) = 57
    c: DistanceX(g5,g5) = 130
    c: DistanceY(g-1,g3) = 10
    c: DistanceX(g3,g3) = 5
    c: Radius(g1) = 5
    c: DistanceY(g2,g0) = 33
FEATURE [PartDesign::Pocket] Pocket345  label="Remove Shell001"
  BaseFeature = -> Pocket349
  Length = 25
  Length2 = 100
  Profile = -> Sketch861
  Type = 0
FEATURE [Sketcher::SketchObject] Sketch863
  MapMode = 5
  Placement = pos=(0,0,25) rot=(0,0,1;0rad)
  Support = -> [Pocket345]
  sketch-geometry (4):
    g0: LineSegment StartX=117 StartY=10 StartZ=0 EndX=125 EndY=10 EndZ=0
    g1: LineSegment StartX=125 StartY=10 StartZ=0 EndX=125 EndY=15 EndZ=0
    g2: LineSegment StartX=125 StartY=15 StartZ=0 EndX=117 EndY=15 EndZ=0
    g3: LineSegment StartX=117 StartY=15 StartZ=0 EndX=117 EndY=10 EndZ=0
  constraints (12):
    c: Coincident(g0,g1)
    c: Coincident(g1,g2)
    c: Coincident(g2,g3)
    c: Coincident(g3,g0)
    c: Horizontal(g0)
    c: Horizontal(g2)
    c: Vertical(g1)
    c: Vertical(g3)
    c: DistanceY(g1,g1) = 5
    c: DistanceX(g2,g2) = 8
    c: DistanceY(g-1,g0) = 10
    c: DistanceX(g-1,g2) = 117
FEATURE [PartDesign::Pocket] Pocket357  label="Remove Shell at Servopocket001"
  BaseFeature = -> Pocket345
  Length = 20
  Length2 = 100
  Profile = -> Sketch863
  Type = 0
FEATURE [Sketcher::SketchObject] Sketch858
  MapMode = 5
  Placement = pos=(125,0,0) rot=(0.57735,0.57735,0.57735;2.0944rad)
  Support = -> [Pocket357]
  sketch-geometry (4):
    g0: LineSegment StartX=29.5 StartY=25 StartZ=0 EndX=34.5 EndY=25 EndZ=0
    g1: LineSegment StartX=29.5 StartY=25 StartZ=0 EndX=29.5 EndY=11.5 EndZ=0
    g2: LineSegment StartX=34.5 StartY=25 StartZ=0 EndX=34.5 EndY=11.5 EndZ=0
    g3: ArcOfCircle CenterX=32 CenterY=11.5 CenterZ=0 NormalX=0 NormalY=0 NormalZ=1 AngleXU=0 Radius=2.5 StartAngle=3.14159 EndAngle=6.28319
  constraints (11):
    c: Horizontal(g0)
    c: Coincident(g1,g0)
    c: Vertical(g1)
    c: Coincident(g2,g0)
    c: Vertical(g2)
    c: Tangent(g3,g1) = -1.5708
    c: Tangent(g3,g2) = 1.5708
    c: DistanceX(g0,g0) = 5
    c: DistanceY(g-1,g3) = 11.5
    c: DistanceX(g-1,g3) = 32
    c: DistanceY(g-1,g0) = 25
FEATURE [PartDesign::Pocket] Pocket340  label="Servocable005"
  BaseFeature = -> Pocket357
  Length = 8
  Length2 = 100
  Profile = -> Sketch858
  Type = 0
FEATURE [Sketcher::SketchObject] Sketch866
  MapMode = 5
  Placement = pos=(125,0,0) rot=(0.57735,0.57735,0.57735;2.0944rad)
  Support = -> [Pocket340]
  sketch-geometry (8):
    g0: LineSegment StartX=18 StartY=22.9 StartZ=0 EndX=21 EndY=22.9 EndZ=0
    g1: LineSegment StartX=21 StartY=22.9 StartZ=0 EndX=21 EndY=17.1 EndZ=0
    g2: LineSegment StartX=21 StartY=17.1 StartZ=0 EndX=18 EndY=17.1 EndZ=0
    g3: LineSegment StartX=18 StartY=17.1 StartZ=0 EndX=18 EndY=22.9 EndZ=0
    g4: LineSegment StartX=18 StartY=12.9 StartZ=0 EndX=21 EndY=12.9 EndZ=0
    g5: LineSegment StartX=21 StartY=12.9 StartZ=0 EndX=21 EndY=7.1 EndZ=0
    g6: LineSegment StartX=21 StartY=7.1 StartZ=0 EndX=18 EndY=7.1 EndZ=0
    g7: LineSegment StartX=18 StartY=7.1 StartZ=0 EndX=18 EndY=12.9 EndZ=0
  constraints (24):
    c: Coincident(g0,g1)
    c: Coincident(g1,g2)
    c: Coincident(g2,g3)
    c: Coincident(g3,g0)
    c: Horizontal(g0)
    c: Horizontal(g2)
    c: Vertical(g1)
    c: Vertical(g3)
    c: Coincident(g4,g5)
    c: Coincident(g5,g6)
    c: Coincident(g6,g7)
    c: Coincident(g7,g4)
    c: Horizontal(g4)
    c: Horizontal(g6)
    c: Vertical(g5)
    c: Vertical(g7)
    c: Equal(g0,g4)
    c: Equal(g1,g5)
    c: Vertical(g4,g2)
    c: DistanceX(g-1,g6) = 18
    c: DistanceX(g6,g6) = 3
    c: DistanceY(g5,g5) = 5.8
    c: DistanceY(g4,g1) = 4.2
    c: DistanceY(g-1,g6) = 7.1
FEATURE [PartDesign::Pocket] Pocket334  label="Nutholes Servopocket001"
  BaseFeature = -> Pocket340
  Length = 56.5
  Length2 = 100
  Profile = -> Sketch866
  Type = 0
FEATURE [Sketcher::SketchObject] Sketch870
  MapMode = 5
  Placement = pos=(0,10,-2.2e-15) rot=(1,0,0;1.5708rad)
  Support = -> [Pocket334]
  sketch-geometry (4):
    g0: Circle CenterX=72.5 CenterY=20 CenterZ=0 NormalX=0 NormalY=0 NormalZ=1 AngleXU=0 Radius=1.6
    g1: Circle CenterX=72.5 CenterY=10 CenterZ=0 NormalX=0 NormalY=0 NormalZ=1 AngleXU=0 Radius=1.6
    g2: Circle CenterX=121 CenterY=20 CenterZ=0 NormalX=0 NormalY=0 NormalZ=1 AngleXU=0 Radius=1.6
    g3: Circle CenterX=121 CenterY=10 CenterZ=0 NormalX=0 NormalY=0 NormalZ=1 AngleXU=0 Radius=1.6
  constraints (12):
    c: Vertical(g3,g2)
    c: Vertical(g1,g0)
    c: Horizontal(g0,g2)
    c: Horizontal(g1,g3)
    c: Equal(g0,g1)
    c: Equal(g1,g2)
    c: Equal(g2,g3)
    c: Radius(g2) = 1.6
    c: DistanceY(g1,g0) = 10
    c: DistanceY(g-1,g1) = 10
    c: DistanceX(g1,g3) = 48.5
    c: DistanceX(g-1,g1) = 72.5
FEATURE [PartDesign::Pocket] Pocket329  label="Screwholes Servopocket002"
  BaseFeature = -> Pocket334
  Length = 18
  Length2 = 100
  Profile = -> Sketch870
  Type = 0
FEATURE [Sketcher::SketchObject] Sketch867
  MapMode = 5
  Placement = pos=(0,5,0) rot=(1,0,0;1.5708rad)
  Support = -> [Pocket329]
  sketch-geometry (3):
    g0: Circle [constr] CenterX=0 CenterY=0 CenterZ=0 NormalX=0 NormalY=0 NormalZ=1 AngleXU=0 Radius=35
    g1: Circle CenterX=33.541 CenterY=10 CenterZ=0 NormalX=0 NormalY=0 NormalZ=1 AngleXU=0 Radius=1.6
    g2: Circle CenterX=28.7228 CenterY=20 CenterZ=0 NormalX=0 NormalY=0 NormalZ=1 AngleXU=0 Radius=1.6
  constraints (8):
    c: Coincident(g0,g-1)
    c: Radius(g0) = 35
    c: PointOnObject(g1,g0)
    c: PointOnObject(g2,g0)
    c: Equal(g2,g1)
    c: Radius(g2) = 1.6
    c: DistanceY(g1,g2) = 10
    c: DistanceY(g-1,g1) = 10
FEATURE [PartDesign::Pocket] Pocket335  label="Screwholes Servohorn Mount002"
  BaseFeature = -> Pocket329
  Length = 20
  Length2 = 100
  Profile = -> Sketch867
  Type = 0
FEATURE [Sketcher::SketchObject] Sketch853
  MapMode = 5
  Placement = pos=(0,43,0) rot=(0,0.707107,0.707107;3.14159rad)
  Support = -> [Pocket335]
  sketch-geometry (3):
    g0: Circle [constr] CenterX=0 CenterY=0 CenterZ=0 NormalX=0 NormalY=0 NormalZ=1 AngleXU=0 Radius=35
    g1: Circle CenterX=-33.541 CenterY=10 CenterZ=0 NormalX=0 NormalY=0 NormalZ=1 AngleXU=0 Radius=1.6
    g2: Circle CenterX=-28.7228 CenterY=20 CenterZ=0 NormalX=0 NormalY=0 NormalZ=1 AngleXU=0 Radius=1.6
  constraints (8):
    c: Coincident(g0,g-1)
    c: Radius(g0) = 35
    c: PointOnObject(g1,g0)
    c: PointOnObject(g2,g0)
    c: Equal(g2,g1)
    c: Radius(g2) = 1.6
    c: DistanceY(g1,g2) = 10
    c: DistanceY(g-1,g1) = 10
FEATURE [PartDesign::Pocket] Pocket339  label="Screwholes Ball Bearing Mount001"
  BaseFeature = -> Pocket335
  Length = 10
  Length2 = 100
  Profile = -> Sketch853
  Type = 0
FEATURE [Sketcher::SketchObject] Sketch852
  MapMode = 5
  Placement = pos=(0,0,25) rot=(0,0,1;0rad)
  Support = -> [Pocket339]
  sketch-geometry (6):
    g0: LineSegment StartX=0 StartY=14 StartZ=0 EndX=40 EndY=14 EndZ=0
    g1: LineSegment StartX=40 StartY=14 StartZ=0 EndX=40 EndY=26 EndZ=0
    g2: LineSegment StartX=0 StartY=31 StartZ=0 EndX=0 EndY=14 EndZ=0
    g3: LineSegment StartX=40 StartY=26 StartZ=0 EndX=67.5 EndY=26 EndZ=0
    g4: LineSegment StartX=67.5 StartY=26 StartZ=0 EndX=67.5 EndY=31 EndZ=0
    g5: LineSegment StartX=67.5 StartY=31 StartZ=0 EndX=0 EndY=31 EndZ=0
  constraints (18):
    c: Coincident(g0,g1)
    c: Coincident(g2,g0)
    c: Horizontal(g0)
    c: Vertical(g1)
    c: Vertical(g2)
    c: PointOnObject(g0,g-2)
    c: DistanceY(g1,g2) = 17
    c: DistanceY(g-1,g0) = 14
    c: Horizontal(g3)
    c: Coincident(g4,g3)
    c: Vertical(g4)
    c: Horizontal(g5)
    c: Coincident(g4,g5)
    c: Coincident(g1,g3)
    c: Coincident(g5,g2)
    c: DistanceX(g-1,g4) = 67.5
    c: DistanceY(g4,g4) = 5
    c: DistanceX(g0,g0) = 40
FEATURE [PartDesign::Pocket] Pocket330  label="Interlock001"
  BaseFeature = -> Pocket339
  Length = 20
  Length2 = 100
  Profile = -> Sketch852
  Type = 0
FEATURE [PartDesign::Pocket] Pocket351  label="Bottom Nuthole Ball Bearing Mount001"
  BaseFeature = -> Pocket330
  Length = 38
  Length2 = 100
  Profile = -> Sketch855
  Reversed = true
  Type = 0
FEATURE [PartDesign::Pocket] Pocket355  label="Top Nuthole Ball Bearing Mount001"
  BaseFeature = -> Pocket351
  Length = 33
  Length2 = 100
  Profile = -> Sketch864
  Reversed = true
  Type = 0
FEATURE [PartDesign::Fillet] Fillet113  label="Smooth Interlock002"
  Base = -> Pocket355 [Edge21,Edge15,Edge85,Edge118,Edge117,Edge116,Edge75,Edge13,Edge76,Edge178,Edge179,Edge88,Edge84,Edge83,Edge82,Edge81,Edge14,Edge72,Edge78,Edge87,Edge86]
  BaseFeature = -> Pocket355
  Radius = 0.4
FEATURE [PartDesign::Fillet] Fillet109  label="Smooth Servopocket001"
  Base = -> Fillet113 [Edge244,Edge256,Edge257,Edge246,Edge255]
  BaseFeature = -> Fillet113
  Radius = 1
FEATURE [PartDesign::Fillet] Fillet103  label="Smooth Servocable Edges003"
  Base = -> Fillet109 [Edge10,Edge199]
  BaseFeature = -> Fillet109
  Radius = 2.5
FEATURE [PartDesign::Body] Body230  label="Limb_Bottom_Shell001"
  Group = -> [Sketch860,Pad360,Pocket346,Pocket352,Sketch874,SubtractivePipe008,Fillet104,Sketch882,Pocket353,Sketch857,Pocket344,Sketch879,Pocket341,Pad361,Fillet105,Sketch873,Pocket342,Fillet106,Sketch865,Pocket349,Sketch861,Pocket345,Sketch863,Pocket357,Sketch858,Pocket340,Sketch866,Pocket334,Sketch870,Pocket329,Sketch867,Pocket335,Sketch853,Pocket339,Sketch852,Pocket330,Sketch855,Pocket351,Sketch864,+4 more]
  Origin = -> Origin360
  Placement = pos=(-144.05,-29.45,42.05) rot=(0,0,1;0rad)
  Tip = -> Fillet103
FEATURE [Sketcher::SketchObject] Sketch884
  MapMode = 5
  Placement = pos=(0,0,0) rot=(0.57735,0.57735,0.57735;2.0944rad)
  Support = -> [YZ_Plane297]
  sketch-geometry (4):
    g0: LineSegment StartX=18.5 StartY=7.1 StartZ=0 EndX=21.5 EndY=7.1 EndZ=0
    g1: LineSegment StartX=21.5 StartY=7.1 StartZ=0 EndX=21.5 EndY=12.9 EndZ=0
    g2: LineSegment StartX=21.5 StartY=12.9 StartZ=0 EndX=18.5 EndY=12.9 EndZ=0
    g3: LineSegment StartX=18.5 StartY=12.9 StartZ=0 EndX=18.5 EndY=7.1 EndZ=0
  constraints (12):
    c: Coincident(g0,g1)
    c: Coincident(g1,g2)
    c: Coincident(g2,g3)
    c: Coincident(g3,g0)
    c: Horizontal(g0)
    c: Horizontal(g2)
    c: Vertical(g1)
    c: Vertical(g3)
    c: DistanceX(g2,g2) = 3
    c: DistanceY(g1,g1) = 5.8
    c: DistanceY(g-1,g0) = 7.1
    c: DistanceX(g-1,g0) = 21.5
FEATURE [Sketcher::SketchObject] Sketch887
  MapMode = 5
  Support = -> [XY_Plane305]
  sketch-geometry (8):
    g0: LineSegment StartX=0 StartY=3.17543 StartZ=0 EndX=-2.75 EndY=1.58771 EndZ=0
    g1: LineSegment StartX=-2.75 StartY=1.58771 StartZ=0 EndX=-2.75 EndY=-1.58771 EndZ=0
    g2: LineSegment StartX=-2.75 StartY=-1.58771 StartZ=0 EndX=0 EndY=-3.17543 EndZ=0
    g3: LineSegment StartX=0 StartY=-3.17543 StartZ=0 EndX=2.75 EndY=-1.58771 EndZ=0
    g4: LineSegment StartX=2.75 StartY=-1.58771 StartZ=0 EndX=2.75 EndY=1.58771 EndZ=0
    g5: LineSegment StartX=2.75 StartY=1.58771 StartZ=0 EndX=0 EndY=3.17543 EndZ=0
    g6: Circle [constr] CenterX=0 CenterY=0 CenterZ=0 NormalX=0 NormalY=0 NormalZ=1 AngleXU=0 Radius=3.17543
    g7: Circle CenterX=0 CenterY=0 CenterZ=0 NormalX=0 NormalY=0 NormalZ=1 AngleXU=0 Radius=1.5
  constraints (18):
    c: Coincident(g0,g1)
    c: Coincident(g1,g2)
    c: Coincident(g2,g3)
    c: Coincident(g3,g4)
    c: Coincident(g4,g5)
    c: Coincident(g5,g0)
    c: Equal(g0, g1-g5) x5
    c: PointOnObject(g0,g6)
    c: PointOnObject(g1,g6)
    c: PointOnObject(g2,g6)
    c: PointOnObject(g3,g6)
    c: PointOnObject(g4,g6)
    c: PointOnObject(g5,g6)
    c: Coincident(g6,g-1)
    c: PointOnObject(g5,g-2)
    c: DistanceX(g0,g4) = 5.5
    c: Coincident(g7,g-1)
    c: Radius(g7) = 1.5
FEATURE [PartDesign::Pad] Pad362  label="M3 Nut Primitive069"
  Length = 1.2
  Length2 = 1.2
  Profile = -> Sketch887
  Type = 4
FEATURE [Sketcher::SketchObject] Sketch886
  ExternalGeometry = -> [Pad362]
  MapMode = 5
  Placement = pos=(0,0,0) rot=(0.57735,0.57735,0.57735;2.0944rad)
  Support = -> [YZ_Plane304]
  sketch-geometry (6):
    g0: LineSegment StartX=-2.67543 StartY=1.2 StartZ=0 EndX=-3.67543 EndY=1.2 EndZ=0
    g1: LineSegment StartX=-3.67543 StartY=1.2 StartZ=0 EndX=-3.67543 EndY=-1.2 EndZ=0
    g2: LineSegment StartX=-3.67543 StartY=-1.2 StartZ=0 EndX=-2.67543 EndY=-1.2 EndZ=0
    g3: LineSegment StartX=-2.67543 StartY=-1.2 StartZ=0 EndX=-3.17543 EndY=-1 EndZ=0
    g4: LineSegment StartX=-3.17543 StartY=-1 StartZ=0 EndX=-3.17543 EndY=1 EndZ=0
    g5: LineSegment StartX=-3.17543 StartY=1 StartZ=0 EndX=-2.67543 EndY=1.2 EndZ=0
  constraints (15):
    c: Horizontal(g0)
    c: Coincident(g0,g1)
    c: Coincident(g1,g2)
    c: Coincident(g2,g3)
    c: Coincident(g3,g4)
    c: Coincident(g4,g5)
    c: Coincident(g5,g0)
    c: Symmetric(g4,g3,g-1)
    c: Symmetric(g0,g2,g-1)
    c: Symmetric(g1,g0,g-1)
    c: DistanceX(g0,g4) = 0.5
    c: DistanceY(g3,g4) = 2
    c: DistanceY(g1,g0) = 2.4
    c: PointOnObject(g3,g-3)
    c: DistanceX(g4,g0) = 0.5
FEATURE [PartDesign::Groove] Groove080  label="M3 Nut Smooth076"
  Angle = 360
  Axis = (-2e-16,3e-16,1)
  Base = (0,0,0)
  BaseFeature = -> Pad362
  Profile = -> Sketch886
  ReferenceAxis = -> Sketch886 [V_Axis]
  Reversed = true
FEATURE [Sketcher::SketchObject] Sketch888
  MapMode = 5
  Placement = pos=(0,0,0) rot=(0.57735,0.57735,0.57735;2.0944rad)
  Support = -> [YZ_Plane297]
  sketch-geometry (4):
    g0: LineSegment StartX=18.5 StartY=17.1 StartZ=0 EndX=21.5 EndY=17.1 EndZ=0
    g1: LineSegment StartX=21.5 StartY=17.1 StartZ=0 EndX=21.5 EndY=22.9 EndZ=0
    g2: LineSegment StartX=21.5 StartY=22.9 StartZ=0 EndX=18.5 EndY=22.9 EndZ=0
    g3: LineSegment StartX=18.5 StartY=22.9 StartZ=0 EndX=18.5 EndY=17.1 EndZ=0
  constraints (12):
    c: Coincident(g0,g1)
    c: Coincident(g1,g2)
    c: Coincident(g2,g3)
    c: Coincident(g3,g0)
    c: Horizontal(g0)
    c: Horizontal(g2)
    c: Vertical(g1)
    c: Vertical(g3)
    c: DistanceX(g2,g2) = 3
    c: DistanceY(g1,g1) = 5.8
    c: DistanceX(g-1,g0) = 21.5
    c: DistanceY(g-1,g0) = 17.1
FEATURE [Sketcher::SketchObject] Sketch891
  MapMode = 5
  Support = -> [XY_Plane303]
  sketch-geometry (8):
    g0: LineSegment StartX=0 StartY=3.17543 StartZ=0 EndX=-2.75 EndY=1.58771 EndZ=0
    g1: LineSegment StartX=-2.75 StartY=1.58771 StartZ=0 EndX=-2.75 EndY=-1.58771 EndZ=0
    g2: LineSegment StartX=-2.75 StartY=-1.58771 StartZ=0 EndX=0 EndY=-3.17543 EndZ=0
    g3: LineSegment StartX=0 StartY=-3.17543 StartZ=0 EndX=2.75 EndY=-1.58771 EndZ=0
    g4: LineSegment StartX=2.75 StartY=-1.58771 StartZ=0 EndX=2.75 EndY=1.58771 EndZ=0
    g5: LineSegment StartX=2.75 StartY=1.58771 StartZ=0 EndX=0 EndY=3.17543 EndZ=0
    g6: Circle [constr] CenterX=0 CenterY=0 CenterZ=0 NormalX=0 NormalY=0 NormalZ=1 AngleXU=0 Radius=3.17543
    g7: Circle CenterX=0 CenterY=0 CenterZ=0 NormalX=0 NormalY=0 NormalZ=1 AngleXU=0 Radius=1.5
  constraints (18):
    c: Coincident(g0,g1)
    c: Coincident(g1,g2)
    c: Coincident(g2,g3)
    c: Coincident(g3,g4)
    c: Coincident(g4,g5)
    c: Coincident(g5,g0)
    c: Equal(g0, g1-g5) x5
    c: PointOnObject(g0,g6)
    c: PointOnObject(g1,g6)
    c: PointOnObject(g2,g6)
    c: PointOnObject(g3,g6)
    c: PointOnObject(g4,g6)
    c: PointOnObject(g5,g6)
    c: Coincident(g6,g-1)
    c: PointOnObject(g5,g-2)
    c: DistanceX(g0,g4) = 5.5
    c: Coincident(g7,g-1)
    c: Radius(g7) = 1.5
FEATURE [PartDesign::Pad] Pad383  label="M3 Nut Primitive075"
  Length = 1.2
  Length2 = 1.2
  Profile = -> Sketch891
  Type = 4
FEATURE [Sketcher::SketchObject] Sketch892
  MapMode = 5
  Support = -> [XY_Plane304]
  sketch-geometry (8):
    g0: LineSegment StartX=0 StartY=3.17543 StartZ=0 EndX=-2.75 EndY=1.58771 EndZ=0
    g1: LineSegment StartX=-2.75 StartY=1.58771 StartZ=0 EndX=-2.75 EndY=-1.58771 EndZ=0
    g2: LineSegment StartX=-2.75 StartY=-1.58771 StartZ=0 EndX=0 EndY=-3.17543 EndZ=0
    g3: LineSegment StartX=0 StartY=-3.17543 StartZ=0 EndX=2.75 EndY=-1.58771 EndZ=0
    g4: LineSegment StartX=2.75 StartY=-1.58771 StartZ=0 EndX=2.75 EndY=1.58771 EndZ=0
    g5: LineSegment StartX=2.75 StartY=1.58771 StartZ=0 EndX=0 EndY=3.17543 EndZ=0
    g6: Circle [constr] CenterX=0 CenterY=0 CenterZ=0 NormalX=0 NormalY=0 NormalZ=1 AngleXU=0 Radius=3.17543
    g7: Circle CenterX=0 CenterY=0 CenterZ=0 NormalX=0 NormalY=0 NormalZ=1 AngleXU=0 Radius=1.5
  constraints (18):
    c: Coincident(g0,g1)
    c: Coincident(g1,g2)
    c: Coincident(g2,g3)
    c: Coincident(g3,g4)
    c: Coincident(g4,g5)
    c: Coincident(g5,g0)
    c: Equal(g0, g1-g5) x5
    c: PointOnObject(g0,g6)
    c: PointOnObject(g1,g6)
    c: PointOnObject(g2,g6)
    c: PointOnObject(g3,g6)
    c: PointOnObject(g4,g6)
    c: PointOnObject(g5,g6)
    c: Coincident(g6,g-1)
    c: PointOnObject(g5,g-2)
    c: DistanceX(g0,g4) = 5.5
    c: Coincident(g7,g-1)
    c: Radius(g7) = 1.5
FEATURE [PartDesign::Pad] Pad365  label="M3 Nut Primitive070"
  Length = 1.2
  Length2 = 1.2
  Profile = -> Sketch892
  Type = 4
FEATURE [PartDesign::Chamfer] Chamfer210  label="M3 Nut Smooth Hole088"
  Base = -> Groove080 [Edge24,Edge23]
  BaseFeature = -> Groove080
  Size = 0.2
FEATURE [PartDesign::Body] Body196  label="M3 Nut033"
  Group = -> [Sketch887,Pad362,Sketch886,Groove080,Chamfer210]
  Origin = -> Origin344
  Placement = pos=(-110.55,7.7,52.05) rot=(0.57735,0.57735,-0.57735;2.0944rad)
  Tip = -> Chamfer210
FEATURE [PartDesign::Fillet] Fillet120  label="Smooth Edges010"
  Base = -> SubtractivePipe009 [Edge20,Edge5]
  BaseFeature = -> SubtractivePipe009
  Radius = 1.5
FEATURE [Sketcher::SketchObject] Sketch875
  MapMode = 5
  Placement = pos=(0,5,0) rot=(1,0,0;1.5708rad)
  Support = -> [Fillet120]
  sketch-geometry (1):
    g0: Circle CenterX=0 CenterY=0 CenterZ=0 NormalX=0 NormalY=0 NormalZ=1 AngleXU=0 Radius=30
  constraints (2):
    c: Coincident(g0,g-1)
    c: Radius(g0) = 30
FEATURE [PartDesign::Pocket] Pocket347  label="Joint Pan002"
  BaseFeature = -> Fillet120
  Length = 47
  Length2 = 100
  Profile = -> Sketch875
  Type = 0
FEATURE [Sketcher::SketchObject] Sketch878
  ExternalGeometry = -> [Pocket347]
  MapMode = 5
  Placement = pos=(0,5,0) rot=(1,0,0;1.5708rad)
  Support = -> [Pocket347]
  sketch-geometry (7):
    g0: ArcOfCircle CenterX=23.5 CenterY=28.2018 CenterZ=0 NormalX=0 NormalY=0 NormalZ=1 AngleXU=0 Radius=1.79818 StartAngle=1.57079 EndAngle=2.66896
    g1: LineSegment StartX=21.8989 StartY=29.0204 StartZ=0 EndX=19.5977 EndY=24.5195 EndZ=0
    g2: ArcOfCircle CenterX=21.1988 CenterY=23.701 CenterZ=0 NormalX=0 NormalY=0 NormalZ=1 AngleXU=0 Radius=1.79818 StartAngle=2.66896 EndAngle=3.98266
    g3: Circle [constr] CenterX=0 CenterY=0 CenterZ=0 NormalX=0 NormalY=0 NormalZ=1 AngleXU=0 Radius=30
    g4: LineSegment StartX=23.5 StartY=30 StartZ=0 EndX=0 EndY=30 EndZ=0
    g5: LineSegment StartX=0 StartY=30 StartZ=0 EndX=0 EndY=22.3607 EndZ=0
    g6: LineSegment StartX=0 StartY=22.3607 StartZ=0 EndX=20 EndY=22.3607 EndZ=0
  constraints (19):
    c: Coincident(g3,g-1)
    c: Radius(g3) = 30
    c: Coincident(g4,g0)
    c: PointOnObject(g4,g3)
    c: Horizontal(g4)
    c: Tangent(g4,g0)
    c: Coincident(g5,g4)
    c: Vertical(g5)
    c: Tangent(g2,g3) = 1.5708
    c: Tangent(g2,g1) = -1.5708
    c: Tangent(g1,g0) = -1.5708
    c: DistanceX(g4,g4) = 23.5
    c: PointOnObject(g4,g-2)
    c: DistanceX(g5,g2) = 20
    c: Equal(g0,g2)
    c: Coincident(g6,g5)
    c: Coincident(g6,g2)
    c: Horizontal(g6)
    c: Horizontal(g-3,g0)
FEATURE [PartDesign::Pocket] Pocket348  label="Shortened Angled Top003"
  BaseFeature = -> Pocket347
  Length = 47
  Length2 = 100
  Profile = -> Sketch878
  Type = 0
FEATURE [PartDesign::Pocket] Pocket359  label="Servoplacement Helper Pocket003"
  BaseFeature = -> Pocket348
  Length = 15
  Length2 = 100
  Profile = -> Sketch868
  Type = 0
FEATURE [PartDesign::Pad] Pad357  label="Servoplacement Helper Pad002"
  BaseFeature = -> Pocket359
  Length = 5
  Length2 = 100
  Profile = -> Pocket359 [Face60]
  Type = 0
FEATURE [PartDesign::Fillet] Fillet121  label="Servoplacement Smooth Edges003"
  Base = -> Pad357 [Edge121,Edge125]
  BaseFeature = -> Pad357
  Radius = 0.4
FEATURE [Sketcher::SketchObject] Sketch883
  MapMode = 5
  Placement = pos=(0,10,-2.2e-15) rot=(1,0,0;1.5708rad)
  Support = -> [Fillet121]
  sketch-geometry (4):
    g0: LineSegment StartX=76.5 StartY=25 StartZ=0 EndX=117 EndY=25 EndZ=0
    g1: LineSegment StartX=117 StartY=25 StartZ=0 EndX=117 EndY=5 EndZ=0
    g2: LineSegment StartX=117 StartY=5 StartZ=0 EndX=76.5 EndY=5 EndZ=0
    g3: LineSegment StartX=76.5 StartY=5 StartZ=0 EndX=76.5 EndY=25 EndZ=0
  constraints (12):
    c: Coincident(g0,g1)
    c: Coincident(g1,g2)
    c: Coincident(g2,g3)
    c: Coincident(g3,g0)
    c: Horizontal(g0)
    c: Horizontal(g2)
    c: Vertical(g1)
    c: Vertical(g3)
    c: DistanceX(g0,g0) = 40.5
    c: DistanceY(g3,g3) = 20
    c: DistanceY(g-1,g2) = 5
    c: DistanceX(g-1,g2) = 76.5
FEATURE [PartDesign::Pocket] Pocket365  label="Servo Pocket006"
  BaseFeature = -> Fillet121
  Length = 30
  Length2 = 100
  Profile = -> Sketch883
  Type = 0
FEATURE [PartDesign::Fillet] Fillet115  label="Smooth Mount Edges003"
  Base = -> Pocket365 [Edge147,Edge146,Edge141,Edge152]
  BaseFeature = -> Pocket365
  Radius = 0.4
FEATURE [Sketcher::SketchObject] Sketch871
  MapMode = 5
  Placement = pos=(0,0,0) rot=(1,0,0;3.14159rad)
  Support = -> [Fillet115]
  sketch-geometry (11):
    g0: LineSegment StartX=0 StartY=-43.25 StartZ=0 EndX=120.25 EndY=-43.25 EndZ=0
    g1: ArcOfCircle CenterX=120.25 CenterY=-38.25 CenterZ=0 NormalX=0 NormalY=0 NormalZ=1 AngleXU=0 Radius=5 StartAngle=4.71239 EndAngle=6.28319
    g2: LineSegment StartX=125.25 StartY=-38.25 StartZ=0 EndX=125.25 EndY=-14.75 EndZ=0
    g3: LineSegment StartX=125.25 StartY=-14.75 StartZ=0 EndX=117 EndY=-14.75 EndZ=0
    g4: LineSegment StartX=117 StartY=-14.75 StartZ=0 EndX=117 EndY=0 EndZ=0
    g5: LineSegment StartX=117 StartY=0 StartZ=0 EndX=0 EndY=0 EndZ=0
    g6: LineSegment StartX=0 StartY=0 StartZ=0 EndX=0 EndY=-14.25 EndZ=0
    g7: LineSegment StartX=0 StartY=-14.25 StartZ=0 EndX=39.75 EndY=-14.25 EndZ=0
    g8: LineSegment StartX=39.75 StartY=-14.25 StartZ=0 EndX=39.75 EndY=-25.75 EndZ=0
    g9: LineSegment StartX=39.75 StartY=-25.75 StartZ=0 EndX=0 EndY=-25.75 EndZ=0
    g10: LineSegment StartX=0 StartY=-25.75 StartZ=0 EndX=0 EndY=-43.25 EndZ=0
  constraints (30):
    c: PointOnObject(g0,g-2)
    c: Horizontal(g0)
    c: Tangent(g0,g1) = -1.5708
    c: Tangent(g1,g2) = -1.5708
    c: Coincident(g2,g3)
    c: Coincident(g3,g4)
    c: Coincident(g4,g5)
    c: Coincident(g5,g-1)
    c: Coincident(g5,g6)
    c: Coincident(g10,g0)
    c: Horizontal(g3)
    c: Vertical(g4)
    c: Vertical(g2)
    c: Horizontal(g5)
    c: DistanceX(g5,g2) = 125.25
    c: Radius(g1) = 5
    c: DistanceY(g4,g4) = 14.75
    c: DistanceX(g3,g3) = 8.25
    c: DistanceY(g0,g4) = 43.25
    c: Horizontal(g7)
    c: Coincident(g7,g8)
    c: Vertical(g8)
    c: Coincident(g8,g9)
    c: Horizontal(g9)
    c: Coincident(g6,g7)
    c: Tangent(g6,g10)
    c: DistanceY(g8,g8) = 11.5
    c: DistanceX(g7,g7) = 39.75
    c: DistanceY(g6,g5) = 14.25
    c: Coincident(g9,g10)
FEATURE [PartDesign::Pocket] Pocket374  label="Bottom Removal and Interlock001"
  BaseFeature = -> Fillet115
  Length = 25
  Length2 = 100
  Profile = -> Sketch871
  Type = 0
FEATURE [Sketcher::SketchObject] Sketch872
  MapMode = 5
  Placement = pos=(0,0,0) rot=(1,0,0;3.14159rad)
  Support = -> [Pocket374]
  sketch-geometry (4):
    g0: LineSegment StartX=0 StartY=-26 StartZ=0 EndX=40 EndY=-26 EndZ=0
    g1: LineSegment StartX=40 StartY=-26 StartZ=0 EndX=40 EndY=-14 EndZ=0
    g2: LineSegment StartX=40 StartY=-14 StartZ=0 EndX=0 EndY=-14 EndZ=0
    g3: LineSegment StartX=0 StartY=-14 StartZ=0 EndX=0 EndY=-26 EndZ=0
  constraints (12):
    c: Coincident(g0,g1)
    c: Coincident(g1,g2)
    c: Coincident(g2,g3)
    c: Coincident(g3,g0)
    c: Horizontal(g0)
    c: Horizontal(g2)
    c: Vertical(g1)
    c: Vertical(g3)
    c: PointOnObject(g0,g-2)
    c: DistanceY(g1,g1) = 12
    c: DistanceY(g2,g-1) = 14
    c: DistanceX(g0,g0) = 40
FEATURE [PartDesign::Pocket] Pocket354  label="Shorten Interlock001"
  BaseFeature = -> Pocket374
  Length = 5
  Length2 = 100
  Profile = -> Sketch872
  Type = 0
FEATURE [Sketcher::SketchObject] Sketch893
  MapMode = 5
  Support = -> [XY_Plane237]
  sketch-geometry (8):
    g0: LineSegment StartX=0 StartY=3.17543 StartZ=0 EndX=-2.75 EndY=1.58771 EndZ=0
    g1: LineSegment StartX=-2.75 StartY=1.58771 StartZ=0 EndX=-2.75 EndY=-1.58771 EndZ=0
    g2: LineSegment StartX=-2.75 StartY=-1.58771 StartZ=0 EndX=0 EndY=-3.17543 EndZ=0
    g3: LineSegment StartX=0 StartY=-3.17543 StartZ=0 EndX=2.75 EndY=-1.58771 EndZ=0
    g4: LineSegment StartX=2.75 StartY=-1.58771 StartZ=0 EndX=2.75 EndY=1.58771 EndZ=0
    g5: LineSegment StartX=2.75 StartY=1.58771 StartZ=0 EndX=0 EndY=3.17543 EndZ=0
    g6: Circle [constr] CenterX=0 CenterY=0 CenterZ=0 NormalX=0 NormalY=0 NormalZ=1 AngleXU=0 Radius=3.17543
    g7: Circle CenterX=0 CenterY=0 CenterZ=0 NormalX=0 NormalY=0 NormalZ=1 AngleXU=0 Radius=1.5
  constraints (18):
    c: Coincident(g0,g1)
    c: Coincident(g1,g2)
    c: Coincident(g2,g3)
    c: Coincident(g3,g4)
    c: Coincident(g4,g5)
    c: Coincident(g5,g0)
    c: Equal(g0, g1-g5) x5
    c: PointOnObject(g0,g6)
    c: PointOnObject(g1,g6)
    c: PointOnObject(g2,g6)
    c: PointOnObject(g3,g6)
    c: PointOnObject(g4,g6)
    c: PointOnObject(g5,g6)
    c: Coincident(g6,g-1)
    c: PointOnObject(g5,g-2)
    c: DistanceX(g0,g4) = 5.5
    c: Coincident(g7,g-1)
    c: Radius(g7) = 1.5
FEATURE [PartDesign::Pad] Pad370  label="M3 Nut Primitive073"
  Length = 1.2
  Length2 = 1.2
  Profile = -> Sketch893
  Type = 4
FEATURE [Sketcher::SketchObject] Sketch896
  MapMode = 5
  Placement = pos=(0,0,0) rot=(1,0,0;3.14159rad)
  Support = -> [Pad366]
  sketch-geometry (1):
    g0: Circle CenterX=0 CenterY=0 CenterZ=0 NormalX=0 NormalY=0 NormalZ=1 AngleXU=0 Radius=2.5
  constraints (2):
    c: Coincident(g0,g-1)
    c: Radius(g0) = 2.5
FEATURE [PartDesign::Pocket] Pocket364
  BaseFeature = -> Pad366
  Length = 5
  Length2 = 100
  Profile = -> Sketch896
  Type = 0
FEATURE [Sketcher::SketchObject] Sketch885
  MapMode = 5
  Placement = pos=(0,0,0) rot=(1,0,0;3.14159rad)
  Support = -> [Pocket364]
  sketch-geometry (2):
    g0: Circle CenterX=0 CenterY=0 CenterZ=0 NormalX=0 NormalY=0 NormalZ=1 AngleXU=0 Radius=3.5
    g1: Circle CenterX=0 CenterY=0 CenterZ=0 NormalX=0 NormalY=0 NormalZ=1 AngleXU=0 Radius=7
  constraints (4):
    c: Coincident(g0,g-1)
    c: Coincident(g1,g0)
    c: Radius(g0) = 3.5
    c: Radius(g1) = 7
FEATURE [PartDesign::Pocket] Pocket362
  BaseFeature = -> Pocket364
  Length = 0.5
  Length2 = 100
  Profile = -> Sketch885
  Type = 0
FEATURE [Sketcher::SketchObject] Sketch890
  MapMode = 5
  Placement = pos=(0,0,5) rot=(0,0,1;0rad)
  Support = -> [Pocket362]
  sketch-geometry (2):
    g0: Circle CenterX=0 CenterY=0 CenterZ=0 NormalX=0 NormalY=0 NormalZ=1 AngleXU=0 Radius=3.5
    g1: Circle CenterX=0 CenterY=0 CenterZ=0 NormalX=0 NormalY=0 NormalZ=1 AngleXU=0 Radius=7
  constraints (4):
    c: Coincident(g0,g-1)
    c: Coincident(g1,g0)
    c: Radius(g0) = 3.5
    c: Radius(g1) = 7
FEATURE [PartDesign::Pocket] Pocket361
  BaseFeature = -> Pocket362
  Length = 0.5
  Length2 = 100
  Profile = -> Sketch890
  Type = 0
FEATURE [PartDesign::Chamfer] Chamfer208
  Base = -> Pocket361 [Face10,Face2,Face3,Face11]
  BaseFeature = -> Pocket361
  Size = 0.25
FEATURE [PartDesign::Body] Body190
  Group = -> [Sketch877,Pad366,Sketch896,Pocket364,Sketch885,Pocket362,Sketch890,Pocket361,Chamfer208]
  Origin = -> Origin341
  Tip = -> Chamfer208
FEATURE [Sketcher::SketchObject] Sketch897
  MapMode = 5
  Placement = pos=(0,52,0) rot=(0,0.707107,0.707107;3.14159rad)
  Support = -> [Pocket354]
  sketch-geometry (3):
    g0: Circle [constr] CenterX=0 CenterY=0 CenterZ=0 NormalX=0 NormalY=0 NormalZ=1 AngleXU=0 Radius=35
    g1: Circle CenterX=-28.7228 CenterY=20 CenterZ=0 NormalX=0 NormalY=0 NormalZ=1 AngleXU=0 Radius=1.6
    g2: Circle CenterX=-33.541 CenterY=10 CenterZ=0 NormalX=0 NormalY=0 NormalZ=1 AngleXU=0 Radius=1.6
  constraints (8):
    c: Coincident(g0,g-1)
    c: Radius(g0) = 35
    c: PointOnObject(g1,g0)
    c: PointOnObject(g2,g0)
    c: Equal(g2,g1)
    c: Radius(g1) = 1.6
    c: DistanceY(g2,g1) = 10
    c: DistanceY(g-1,g2) = 10
FEATURE [PartDesign::Pocket] Pocket350  label="Screwholes Ball Bearing Mount (Interlock)001"
  BaseFeature = -> Pocket354
  Length = 22
  Length2 = 100
  Profile = -> Sketch897
  Type = 0
FEATURE [Sketcher::SketchObject] Sketch880
  MapMode = 5
  Placement = pos=(0,14.25,0) rot=(1,0,0;1.5708rad)
  Support = -> [Pocket350]
  sketch-geometry (3):
    g0: Circle [constr] CenterX=0 CenterY=0 CenterZ=0 NormalX=0 NormalY=0 NormalZ=1 AngleXU=0 Radius=35
    g1: Circle CenterX=28.7228 CenterY=20 CenterZ=0 NormalX=0 NormalY=0 NormalZ=1 AngleXU=0 Radius=1.6
    g2: Circle CenterX=33.541 CenterY=10 CenterZ=0 NormalX=0 NormalY=0 NormalZ=1 AngleXU=0 Radius=1.6
  constraints (8):
    c: Coincident(g0,g-1)
    c: PointOnObject(g1,g0)
    c: PointOnObject(g2,g0)
    c: Equal(g2,g1)
    c: Radius(g1) = 1.6
    c: DistanceY(g2,g1) = 10
    c: DistanceY(g-1,g2) = 10
    c: Radius(g0) = 35
FEATURE [PartDesign::Pocket] Pocket360  label="Screwholes Servohorn Mount003"
  BaseFeature = -> Pocket350
  Length = 10
  Length2 = 100
  Profile = -> Sketch880
  Type = 0
FEATURE [PartDesign::Pocket] Pocket356  label="Bottom Nuthole Ball Bearing Mount (Interlock)001"
  BaseFeature = -> Pocket360
  Length = 38
  Length2 = 100
  Profile = -> Sketch884
  Reversed = true
  Type = 0
FEATURE [PartDesign::Pocket] Pocket372  label="Top Nuthole Ball Bearing Mount (Interlock)001"
  BaseFeature = -> Pocket356
  Length = 33
  Length2 = 100
  Profile = -> Sketch888
  Reversed = true
  Type = 0
FEATURE [Sketcher::SketchObject] Sketch889
  MapMode = 5
  Placement = pos=(0,10,-2.2e-15) rot=(1,0,0;1.5708rad)
  Support = -> [Pocket372]
  sketch-geometry (2):
    g0: Circle CenterX=121 CenterY=20 CenterZ=0 NormalX=0 NormalY=0 NormalZ=1 AngleXU=0 Radius=1.6
    g1: Circle CenterX=121 CenterY=10 CenterZ=0 NormalX=0 NormalY=0 NormalZ=1 AngleXU=0 Radius=1.6
  constraints (6):
    c: Vertical(g1,g0)
    c: Equal(g0,g1)
    c: Radius(g0) = 1.6
    c: DistanceY(g1,g0) = 10
    c: DistanceX(g-1,g1) = 121
    c: DistanceY(g-1,g1) = 10
FEATURE [PartDesign::Pocket] Pocket363  label="Screwholes Servopocket003"
  BaseFeature = -> Pocket372
  Length = 6
  Length2 = 100
  Profile = -> Sketch889
  Type = 0
FEATURE [Sketcher::SketchObject] Sketch894
  MapMode = 5
  Placement = pos=(0,0,25) rot=(1,0,0;3.14159rad)
  Support = -> [Pocket363]
  sketch-geometry (4):
    g0: LineSegment StartX=125 StartY=-26 StartZ=0 EndX=125 EndY=-34.5 EndZ=0
    g1: LineSegment StartX=125 StartY=-34.5 StartZ=0 EndX=30 EndY=-34.5 EndZ=0
    g2: LineSegment StartX=30 StartY=-26 StartZ=0 EndX=125 EndY=-26 EndZ=0
    g3: LineSegment StartX=30 StartY=-34.5 StartZ=0 EndX=30 EndY=-26 EndZ=0
  constraints (12):
    c: Coincident(g0,g1)
    c: Horizontal(g1)
    c: Vertical(g0)
    c: DistanceX(g-1,g0) = 125
    c: Coincident(g3,g2)
    c: Horizontal(g2)
    c: Vertical(g3)
    c: DistanceY(g3,g3) = 8.5
    c: DistanceY(g2,g-1) = 26
    c: DistanceX(g-1,g2) = 30
    c: Coincident(g3,g1)
    c: Coincident(g0,g2)
FEATURE [PartDesign::Pocket] Pocket366  label="Cableguide001"
  BaseFeature = -> Pocket363
  Length = 2
  Length2 = 100
  Profile = -> Sketch894
  Type = 0
FEATURE [PartDesign::Fillet] Fillet119  label="Smooth Corners Cableguide001"
  Base = -> Pocket366 [Edge183,Edge184,Edge188,Edge186]
  BaseFeature = -> Pocket366
  Radius = 1
FEATURE [PartDesign::Fillet] Fillet116  label="Smooth Interlock003"
  Base = -> Fillet119 [Edge89,Edge85,Edge79,Edge86,Edge78,Edge148,Edge80,Edge87,Edge27,Edge23,Edge25,Edge84]
  BaseFeature = -> Fillet119
  Radius = 0.2
FEATURE [Sketcher::SketchObject] Sketch899
  MapMode = 5
  Support = -> [XY_Plane302]
  sketch-geometry (2):
    g0: Circle CenterX=0 CenterY=0 CenterZ=0 NormalX=0 NormalY=0 NormalZ=1 AngleXU=0 Radius=4
    g1: Circle CenterX=0 CenterY=0 CenterZ=0 NormalX=0 NormalY=0 NormalZ=1 AngleXU=0 Radius=6.25
  constraints (4):
    c: Coincident(g0,g-1)
    c: Coincident(g1,g0)
    c: Radius(g0) = 4
    c: Radius(g1) = 6.25
FEATURE [PartDesign::Pad] Pad363
  Length = 5
  Length2 = 100
  Profile = -> Sketch899
  Type = 0
FEATURE [PartDesign::Chamfer] Chamfer199
  Base = -> Pad363 [Face3,Face4]
  BaseFeature = -> Pad363
  Size = 0.2
FEATURE [PartDesign::Body] Body205
  Group = -> [Sketch899,Pad363,Chamfer199]
  Origin = -> Origin377
  Tip = -> Chamfer199
FEATURE [App::Part] Part095  label="Ball Bearing001"
  Group = -> [Body190,Body205,Body203]
  Origin = -> Origin347
  Placement = pos=(-144.1,26.5,26.95) rot=(1,0,0;1.5708rad)
FEATURE [Sketcher::SketchObject] Sketch900
  ExternalGeometry = -> [Pad383]
  MapMode = 5
  Placement = pos=(0,0,0) rot=(0.57735,0.57735,0.57735;2.0944rad)
  Support = -> [YZ_Plane302]
  sketch-geometry (6):
    g0: LineSegment StartX=-2.67543 StartY=1.2 StartZ=0 EndX=-3.67543 EndY=1.2 EndZ=0
    g1: LineSegment StartX=-3.67543 StartY=1.2 StartZ=0 EndX=-3.67543 EndY=-1.2 EndZ=0
    g2: LineSegment StartX=-3.67543 StartY=-1.2 StartZ=0 EndX=-2.67543 EndY=-1.2 EndZ=0
    g3: LineSegment StartX=-2.67543 StartY=-1.2 StartZ=0 EndX=-3.17543 EndY=-1 EndZ=0
    g4: LineSegment StartX=-3.17543 StartY=-1 StartZ=0 EndX=-3.17543 EndY=1 EndZ=0
    g5: LineSegment StartX=-3.17543 StartY=1 StartZ=0 EndX=-2.67543 EndY=1.2 EndZ=0
  constraints (15):
    c: Horizontal(g0)
    c: Coincident(g0,g1)
    c: Coincident(g1,g2)
    c: Coincident(g2,g3)
    c: Coincident(g3,g4)
    c: Coincident(g4,g5)
    c: Coincident(g5,g0)
    c: Symmetric(g4,g3,g-1)
    c: Symmetric(g0,g2,g-1)
    c: Symmetric(g1,g0,g-1)
    c: DistanceX(g0,g4) = 0.5
    c: DistanceY(g3,g4) = 2
    c: DistanceY(g1,g0) = 2.4
    c: PointOnObject(g3,g-3)
    c: DistanceX(g4,g0) = 0.5
FEATURE [PartDesign::Groove] Groove073  label="M3 Nut Smooth069"
  Angle = 360
  Axis = (-2e-16,3e-16,1)
  Base = (0,0,0)
  BaseFeature = -> Pad383
  Profile = -> Sketch900
  ReferenceAxis = -> Sketch900 [V_Axis]
  Reversed = true
FEATURE [PartDesign::Chamfer] Chamfer200  label="M3 Nut Smooth Hole083"
  Base = -> Groove073 [Edge24,Edge23]
  BaseFeature = -> Groove073
  Size = 0.2
FEATURE [PartDesign::Body] Body192  label="M3 Nut032"
  Group = -> [Sketch891,Pad383,Sketch900,Groove073,Chamfer200]
  Origin = -> Origin378
  Placement = pos=(-115.35,7.7,62.05) rot=(0.57735,0.57735,-0.57735;2.0944rad)
  Tip = -> Chamfer200
FEATURE [Sketcher::SketchObject] Sketch901
  MapMode = 5
  Support = -> [XY_Plane300]
  sketch-geometry (8):
    g0: LineSegment StartX=0 StartY=3.17543 StartZ=0 EndX=-2.75 EndY=1.58771 EndZ=0
    g1: LineSegment StartX=-2.75 StartY=1.58771 StartZ=0 EndX=-2.75 EndY=-1.58771 EndZ=0
    g2: LineSegment StartX=-2.75 StartY=-1.58771 StartZ=0 EndX=0 EndY=-3.17543 EndZ=0
    g3: LineSegment StartX=0 StartY=-3.17543 StartZ=0 EndX=2.75 EndY=-1.58771 EndZ=0
    g4: LineSegment StartX=2.75 StartY=-1.58771 StartZ=0 EndX=2.75 EndY=1.58771 EndZ=0
    g5: LineSegment StartX=2.75 StartY=1.58771 StartZ=0 EndX=0 EndY=3.17543 EndZ=0
    g6: Circle [constr] CenterX=0 CenterY=0 CenterZ=0 NormalX=0 NormalY=0 NormalZ=1 AngleXU=0 Radius=3.17543
    g7: Circle CenterX=0 CenterY=0 CenterZ=0 NormalX=0 NormalY=0 NormalZ=1 AngleXU=0 Radius=1.5
  constraints (18):
    c: Coincident(g0,g1)
    c: Coincident(g1,g2)
    c: Coincident(g2,g3)
    c: Coincident(g3,g4)
    c: Coincident(g4,g5)
    c: Coincident(g5,g0)
    c: Equal(g0, g1-g5) x5
    c: PointOnObject(g0,g6)
    c: PointOnObject(g1,g6)
    c: PointOnObject(g2,g6)
    c: PointOnObject(g3,g6)
    c: PointOnObject(g4,g6)
    c: PointOnObject(g5,g6)
    c: Coincident(g6,g-1)
    c: PointOnObject(g5,g-2)
    c: DistanceX(g0,g4) = 5.5
    c: Coincident(g7,g-1)
    c: Radius(g7) = 1.5
FEATURE [PartDesign::Pad] Pad384  label="M3 Nut Primitive076"
  Length = 1.2
  Length2 = 1.2
  Profile = -> Sketch901
  Type = 4
FEATURE [Sketcher::SketchObject] Sketch902
  ExternalGeometry = -> [Pad384]
  MapMode = 5
  Placement = pos=(0,0,0) rot=(0.57735,0.57735,0.57735;2.0944rad)
  Support = -> [YZ_Plane301]
  sketch-geometry (6):
    g0: LineSegment StartX=-2.67543 StartY=1.2 StartZ=0 EndX=-3.67543 EndY=1.2 EndZ=0
    g1: LineSegment StartX=-3.67543 StartY=1.2 StartZ=0 EndX=-3.67543 EndY=-1.2 EndZ=0
    g2: LineSegment StartX=-3.67543 StartY=-1.2 StartZ=0 EndX=-2.67543 EndY=-1.2 EndZ=0
    g3: LineSegment StartX=-2.67543 StartY=-1.2 StartZ=0 EndX=-3.17543 EndY=-1 EndZ=0
    g4: LineSegment StartX=-3.17543 StartY=-1 StartZ=0 EndX=-3.17543 EndY=1 EndZ=0
    g5: LineSegment StartX=-3.17543 StartY=1 StartZ=0 EndX=-2.67543 EndY=1.2 EndZ=0
  constraints (15):
    c: Horizontal(g0)
    c: Coincident(g0,g1)
    c: Coincident(g1,g2)
    c: Coincident(g2,g3)
    c: Coincident(g3,g4)
    c: Coincident(g4,g5)
    c: Coincident(g5,g0)
    c: Symmetric(g4,g3,g-1)
    c: Symmetric(g0,g2,g-1)
    c: Symmetric(g1,g0,g-1)
    c: DistanceX(g0,g4) = 0.5
    c: DistanceY(g3,g4) = 2
    c: DistanceY(g1,g0) = 2.4
    c: PointOnObject(g3,g-3)
    c: DistanceX(g4,g0) = 0.5
FEATURE [PartDesign::Groove] Groove076  label="M3 Nut Smooth072"
  Angle = 360
  Axis = (-2e-16,3e-16,1)
  Base = (0,0,0)
  BaseFeature = -> Pad384
  Profile = -> Sketch902
  ReferenceAxis = -> Sketch902 [V_Axis]
  Reversed = true
FEATURE [PartDesign::Chamfer] Chamfer209  label="M3 Nut Smooth Hole087"
  Base = -> Groove076 [Edge24,Edge23]
  BaseFeature = -> Groove076
  Size = 0.2
FEATURE [PartDesign::Body] Body228  label="M3 Nut041"
  Group = -> [Sketch901,Pad384,Sketch902,Groove076,Chamfer209]
  Origin = -> Origin316
  Placement = pos=(-115.35,-9.3,62.1) rot=(0.57735,0.57735,-0.57735;2.0944rad)
  Tip = -> Chamfer209
FEATURE [Sketcher::SketchObject] Sketch903
  MapMode = 5
  Placement = pos=(130,0,0) rot=(0.57735,0.57735,0.57735;2.0944rad)
  Support = -> [Fillet116]
  sketch-geometry (9):
    g0: LineSegment StartX=30.75 StartY=19.75 StartZ=0 EndX=33.25 EndY=19.75 EndZ=0
    g1: LineSegment StartX=34.5 StartY=18.5 StartZ=0 EndX=34.5 EndY=11.5 EndZ=0
    g2: LineSegment StartX=33.25 StartY=10.25 StartZ=0 EndX=30.75 EndY=10.25 EndZ=0
    g3: LineSegment StartX=29.5 StartY=11.5 StartZ=0 EndX=29.5 EndY=18.5 EndZ=0
    g4: ArcOfCircle CenterX=30.75 CenterY=18.5 CenterZ=0 NormalX=0 NormalY=0 NormalZ=1 AngleXU=0 Radius=1.25 StartAngle=1.5708 EndAngle=3.14159
    g5: ArcOfCircle CenterX=33.25 CenterY=18.5 CenterZ=0 NormalX=0 NormalY=0 NormalZ=1 AngleXU=0 Radius=1.25 StartAngle=1e-16 EndAngle=1.5708
    g6: ArcOfCircle CenterX=33.25 CenterY=11.5 CenterZ=0 NormalX=0 NormalY=0 NormalZ=1 AngleXU=0 Radius=1.25 StartAngle=4.71239 EndAngle=6.28319
    g7: ArcOfCircle CenterX=30.75 CenterY=11.5 CenterZ=0 NormalX=0 NormalY=0 NormalZ=1 AngleXU=0 Radius=1.25 StartAngle=3.14159 EndAngle=4.71239
    g8: Circle [constr] CenterX=32 CenterY=15 CenterZ=0 NormalX=0 NormalY=0 NormalZ=1 AngleXU=0 Radius=2.5
  constraints (23):
    c: Horizontal(g0)
    c: Horizontal(g2)
    c: Vertical(g1)
    c: Vertical(g3)
    c: Tangent(g3,g4) = 1.5708
    c: Tangent(g0,g4) = 1.5708
    c: Tangent(g0,g5) = 1.5708
    c: Tangent(g1,g5) = 1.5708
    c: Tangent(g1,g6) = 1.5708
    c: Tangent(g2,g6) = 1.5708
    c: Tangent(g3,g7) = 1.5708
    c: Tangent(g2,g7) = 1.5708
    c: DistanceY(g2,g0) = 9.5
    c: DistanceX(g3,g1) = 5
    c: Tangent(g8,g3)
    c: Tangent(g8,g1)
    c: Equal(g5,g4)
    c: Equal(g4,g7)
    c: Equal(g7,g6)
    c: Radius(g5) = 1.25
    c: DistanceY(g8,g0) = 4.75
    c: DistanceX(g-1,g8) = 32
    c: DistanceY(g-1,g8) = 15
FEATURE [PartDesign::Pocket] Pocket371  label="Servocable006"
  BaseFeature = -> Fillet116
  Length = 5
  Length2 = 100
  Profile = -> Sketch903
  Type = 0
FEATURE [Sketcher::SketchObject] Sketch898
  MapMode = 5
  Placement = pos=(0,0,0) rot=(1,0,0;3.14159rad)
  Support = -> [Pocket371]
  sketch-geometry (4):
    g0: LineSegment StartX=117 StartY=-15 StartZ=0 EndX=125.25 EndY=-15 EndZ=0
    g1: LineSegment StartX=125.25 StartY=-15 StartZ=0 EndX=125.25 EndY=-10 EndZ=0
    g2: LineSegment StartX=125.25 StartY=-10 StartZ=0 EndX=117 EndY=-10 EndZ=0
    g3: LineSegment StartX=117 StartY=-10 StartZ=0 EndX=117 EndY=-15 EndZ=0
  constraints (12):
    c: Coincident(g0,g1)
    c: Coincident(g1,g2)
    c: Coincident(g2,g3)
    c: Coincident(g3,g0)
    c: Horizontal(g0)
    c: Horizontal(g2)
    c: Vertical(g1)
    c: Vertical(g3)
    c: DistanceX(g2,g2) = 8.25
    c: DistanceY(g3,g3) = 5
    c: DistanceY(g2,g-1) = 10
    c: DistanceX(g-1,g2) = 117
FEATURE [PartDesign::Pocket] Pocket368  label="Servopocket Interlock001"
  BaseFeature = -> Pocket371
  Length = 5
  Length2 = 100
  Profile = -> Sketch898
  Type = 0
FEATURE [PartDesign::Body] Body195  label="Limb_Top_Shell001"
  Group = -> [Sketch881,Pad358,Pocket343,Pocket358,Sketch876,SubtractivePipe009,Fillet120,Sketch875,Pocket347,Sketch878,Pocket348,Sketch868,Pocket359,Pad357,Fillet121,Sketch883,Pocket365,Fillet115,Sketch871,Pocket374,Sketch872,Pocket354,Sketch897,Pocket350,Sketch880,Pocket360,Sketch884,Pocket356,Sketch888,Pocket372,Sketch889,Pocket363,Sketch894,Pocket366,Fillet119,Fillet116,Sketch903,Pocket371,Sketch898,+1 more]
  Origin = -> Origin374
  Placement = pos=(-144.1,-29.45,42.1) rot=(0,0,1;0rad)
  Tip = -> Pocket368
FEATURE [Sketcher::SketchObject] Sketch904
  ExternalGeometry = -> [Pad370]
  MapMode = 5
  Placement = pos=(0,0,0) rot=(0.57735,0.57735,0.57735;2.0944rad)
  Support = -> [YZ_Plane237]
  sketch-geometry (6):
    g0: LineSegment StartX=-2.67543 StartY=1.2 StartZ=0 EndX=-3.67543 EndY=1.2 EndZ=0
    g1: LineSegment StartX=-3.67543 StartY=1.2 StartZ=0 EndX=-3.67543 EndY=-1.2 EndZ=0
    g2: LineSegment StartX=-3.67543 StartY=-1.2 StartZ=0 EndX=-2.67543 EndY=-1.2 EndZ=0
    g3: LineSegment StartX=-2.67543 StartY=-1.2 StartZ=0 EndX=-3.17543 EndY=-1 EndZ=0
    g4: LineSegment StartX=-3.17543 StartY=-1 StartZ=0 EndX=-3.17543 EndY=1 EndZ=0
    g5: LineSegment StartX=-3.17543 StartY=1 StartZ=0 EndX=-2.67543 EndY=1.2 EndZ=0
  constraints (15):
    c: Horizontal(g0)
    c: Coincident(g0,g1)
    c: Coincident(g1,g2)
    c: Coincident(g2,g3)
    c: Coincident(g3,g4)
    c: Coincident(g4,g5)
    c: Coincident(g5,g0)
    c: Symmetric(g4,g3,g-1)
    c: Symmetric(g0,g2,g-1)
    c: Symmetric(g1,g0,g-1)
    c: DistanceX(g0,g4) = 0.5
    c: DistanceY(g3,g4) = 2
    c: DistanceY(g1,g0) = 2.4
    c: PointOnObject(g3,g-3)
    c: DistanceX(g4,g0) = 0.5
FEATURE [PartDesign::Groove] Groove077  label="M3 Nut Smooth073"
  Angle = 360
  Axis = (-2e-16,3e-16,1)
  Base = (0,0,0)
  BaseFeature = -> Pad370
  Profile = -> Sketch904
  ReferenceAxis = -> Sketch904 [V_Axis]
  Reversed = true
FEATURE [PartDesign::Chamfer] Chamfer198  label="M3 Nut Smooth Hole082"
  Base = -> Groove077 [Edge24,Edge23]
  BaseFeature = -> Groove077
  Size = 0.2
FEATURE [PartDesign::Body] Body223  label="M3 Nut039"
  Group = -> [Sketch893,Pad370,Sketch904,Groove077,Chamfer198]
  Origin = -> Origin355
  Placement = pos=(-71.6,-9.85,52.05) rot=(0.57735,-0.57735,0.57735;2.0944rad)
  Tip = -> Chamfer198
FEATURE [Sketcher::SketchObject] Sketch910
  MapMode = 5
  Placement = pos=(0,0,0) rot=(1,0,0;1.5708rad)
  Support = -> [XZ_Plane319]
  sketch-geometry (1):
    g0: Circle CenterX=1.55 CenterY=4 CenterZ=0 NormalX=0 NormalY=0 NormalZ=1 AngleXU=0 Radius=0.75
  constraints (3):
    c: Radius(g0) = 0.75
    c: DistanceY(g-1,g0) = 4
    c: DistanceX(g-1,g0) = 1.55
FEATURE [PartDesign::Pad] Pad369
  Length = 10
  Length2 = 100
  Placement = pos=(0,0,0) rot=(1,0,0;1.5708rad)
  Profile = -> Sketch910
  Reversed = true
  Type = 0
FEATURE [PartDesign::Body] Body191  label="brown wire006"
  Group = -> [Sketch910,Pad369]
  Origin = -> Origin379
  Placement = pos=(0,25.15,0) rot=(0,0,1;0rad)
  Tip = -> Pad369
FEATURE [Sketcher::SketchObject] Sketch911
  MapMode = 5
  Support = -> [XY_Plane307]
  sketch-geometry (8):
    g0: LineSegment StartX=0 StartY=3.17543 StartZ=0 EndX=-2.75 EndY=1.58771 EndZ=0
    g1: LineSegment StartX=-2.75 StartY=1.58771 StartZ=0 EndX=-2.75 EndY=-1.58771 EndZ=0
    g2: LineSegment StartX=-2.75 StartY=-1.58771 StartZ=0 EndX=0 EndY=-3.17543 EndZ=0
    g3: LineSegment StartX=0 StartY=-3.17543 StartZ=0 EndX=2.75 EndY=-1.58771 EndZ=0
    g4: LineSegment StartX=2.75 StartY=-1.58771 StartZ=0 EndX=2.75 EndY=1.58771 EndZ=0
    g5: LineSegment StartX=2.75 StartY=1.58771 StartZ=0 EndX=0 EndY=3.17543 EndZ=0
    g6: Circle [constr] CenterX=0 CenterY=0 CenterZ=0 NormalX=0 NormalY=0 NormalZ=1 AngleXU=0 Radius=3.17543
    g7: Circle CenterX=0 CenterY=0 CenterZ=0 NormalX=0 NormalY=0 NormalZ=1 AngleXU=0 Radius=1.5
  constraints (18):
    c: Coincident(g0,g1)
    c: Coincident(g1,g2)
    c: Coincident(g2,g3)
    c: Coincident(g3,g4)
    c: Coincident(g4,g5)
    c: Coincident(g5,g0)
    c: Equal(g0, g1-g5) x5
    c: PointOnObject(g0,g6)
    c: PointOnObject(g1,g6)
    c: PointOnObject(g2,g6)
    c: PointOnObject(g3,g6)
    c: PointOnObject(g4,g6)
    c: PointOnObject(g5,g6)
    c: Coincident(g6,g-1)
    c: PointOnObject(g5,g-2)
    c: DistanceX(g0,g4) = 5.5
    c: Coincident(g7,g-1)
    c: Radius(g7) = 1.5
FEATURE [PartDesign::Pad] Pad371  label="M3 Nut Primitive074"
  Length = 1.2
  Length2 = 1.2
  Profile = -> Sketch911
  Type = 4
FEATURE [Sketcher::SketchObject] Sketch909
  ExternalGeometry = -> [Pad371]
  MapMode = 5
  Placement = pos=(0,0,0) rot=(0.57735,0.57735,0.57735;2.0944rad)
  Support = -> [YZ_Plane303]
  sketch-geometry (6):
    g0: LineSegment StartX=-2.67543 StartY=1.2 StartZ=0 EndX=-3.67543 EndY=1.2 EndZ=0
    g1: LineSegment StartX=-3.67543 StartY=1.2 StartZ=0 EndX=-3.67543 EndY=-1.2 EndZ=0
    g2: LineSegment StartX=-3.67543 StartY=-1.2 StartZ=0 EndX=-2.67543 EndY=-1.2 EndZ=0
    g3: LineSegment StartX=-2.67543 StartY=-1.2 StartZ=0 EndX=-3.17543 EndY=-1 EndZ=0
    g4: LineSegment StartX=-3.17543 StartY=-1 StartZ=0 EndX=-3.17543 EndY=1 EndZ=0
    g5: LineSegment StartX=-3.17543 StartY=1 StartZ=0 EndX=-2.67543 EndY=1.2 EndZ=0
  constraints (15):
    c: Horizontal(g0)
    c: Coincident(g0,g1)
    c: Coincident(g1,g2)
    c: Coincident(g2,g3)
    c: Coincident(g3,g4)
    c: Coincident(g4,g5)
    c: Coincident(g5,g0)
    c: Symmetric(g4,g3,g-1)
    c: Symmetric(g0,g2,g-1)
    c: Symmetric(g1,g0,g-1)
    c: DistanceX(g0,g4) = 0.5
    c: DistanceY(g3,g4) = 2
    c: DistanceY(g1,g0) = 2.4
    c: PointOnObject(g3,g-3)
    c: DistanceX(g4,g0) = 0.5
FEATURE [PartDesign::Groove] Groove078  label="M3 Nut Smooth074"
  Angle = 360
  Axis = (-2e-16,3e-16,1)
  Base = (0,0,0)
  BaseFeature = -> Pad371
  Profile = -> Sketch909
  ReferenceAxis = -> Sketch909 [V_Axis]
  Reversed = true
FEATURE [PartDesign::Chamfer] Chamfer197  label="M3 Nut Smooth Hole081"
  Base = -> Groove078 [Edge24,Edge23]
  BaseFeature = -> Groove078
  Size = 0.2
FEATURE [PartDesign::Body] Body233  label="M3 Nut043"
  Group = -> [Sketch911,Pad371,Sketch909,Groove078,Chamfer197]
  Origin = -> Origin353
  Placement = pos=(-71.5,-9.8,62.05) rot=(0.57735,-0.57735,0.57735;2.0944rad)
  Tip = -> Chamfer197
FEATURE [Sketcher::SketchObject] Sketch913
  MapMode = 5
  Support = -> [XY_Plane298]
  sketch-geometry (8):
    g0: LineSegment StartX=0 StartY=3.17543 StartZ=0 EndX=-2.75 EndY=1.58771 EndZ=0
    g1: LineSegment StartX=-2.75 StartY=1.58771 StartZ=0 EndX=-2.75 EndY=-1.58771 EndZ=0
    g2: LineSegment StartX=-2.75 StartY=-1.58771 StartZ=0 EndX=0 EndY=-3.17543 EndZ=0
    g3: LineSegment StartX=0 StartY=-3.17543 StartZ=0 EndX=2.75 EndY=-1.58771 EndZ=0
    g4: LineSegment StartX=2.75 StartY=-1.58771 StartZ=0 EndX=2.75 EndY=1.58771 EndZ=0
    g5: LineSegment StartX=2.75 StartY=1.58771 StartZ=0 EndX=0 EndY=3.17543 EndZ=0
    g6: Circle [constr] CenterX=0 CenterY=0 CenterZ=0 NormalX=0 NormalY=0 NormalZ=1 AngleXU=0 Radius=3.17543
    g7: Circle CenterX=0 CenterY=0 CenterZ=0 NormalX=0 NormalY=0 NormalZ=1 AngleXU=0 Radius=1.5
  constraints (18):
    c: Coincident(g0,g1)
    c: Coincident(g1,g2)
    c: Coincident(g2,g3)
    c: Coincident(g3,g4)
    c: Coincident(g4,g5)
    c: Coincident(g5,g0)
    c: Equal(g0, g1-g5) x5
    c: PointOnObject(g0,g6)
    c: PointOnObject(g1,g6)
    c: PointOnObject(g2,g6)
    c: PointOnObject(g3,g6)
    c: PointOnObject(g4,g6)
    c: PointOnObject(g5,g6)
    c: Coincident(g6,g-1)
    c: PointOnObject(g5,g-2)
    c: DistanceX(g0,g4) = 5.5
    c: Coincident(g7,g-1)
    c: Radius(g7) = 1.5
FEATURE [PartDesign::Pad] Pad367  label="M3 Nut Primitive071"
  Length = 1.2
  Length2 = 1.2
  Profile = -> Sketch913
  Type = 4
FEATURE [Sketcher::SketchObject] Sketch907
  ExternalGeometry = -> [Pad367]
  MapMode = 5
  Placement = pos=(0,0,0) rot=(0.57735,0.57735,0.57735;2.0944rad)
  Support = -> [YZ_Plane305]
  sketch-geometry (6):
    g0: LineSegment StartX=-2.67543 StartY=1.2 StartZ=0 EndX=-3.67543 EndY=1.2 EndZ=0
    g1: LineSegment StartX=-3.67543 StartY=1.2 StartZ=0 EndX=-3.67543 EndY=-1.2 EndZ=0
    g2: LineSegment StartX=-3.67543 StartY=-1.2 StartZ=0 EndX=-2.67543 EndY=-1.2 EndZ=0
    g3: LineSegment StartX=-2.67543 StartY=-1.2 StartZ=0 EndX=-3.17543 EndY=-1 EndZ=0
    g4: LineSegment StartX=-3.17543 StartY=-1 StartZ=0 EndX=-3.17543 EndY=1 EndZ=0
    g5: LineSegment StartX=-3.17543 StartY=1 StartZ=0 EndX=-2.67543 EndY=1.2 EndZ=0
  constraints (15):
    c: Horizontal(g0)
    c: Coincident(g0,g1)
    c: Coincident(g1,g2)
    c: Coincident(g2,g3)
    c: Coincident(g3,g4)
    c: Coincident(g4,g5)
    c: Coincident(g5,g0)
    c: Symmetric(g4,g3,g-1)
    c: Symmetric(g0,g2,g-1)
    c: Symmetric(g1,g0,g-1)
    c: DistanceX(g0,g4) = 0.5
    c: DistanceY(g3,g4) = 2
    c: DistanceY(g1,g0) = 2.4
    c: PointOnObject(g3,g-3)
    c: DistanceX(g4,g0) = 0.5
FEATURE [PartDesign::Groove] Groove079  label="M3 Nut Smooth075"
  Angle = 360
  Axis = (-2e-16,3e-16,1)
  Base = (0,0,0)
  BaseFeature = -> Pad367
  Profile = -> Sketch907
  ReferenceAxis = -> Sketch907 [V_Axis]
  Reversed = true
FEATURE [PartDesign::Chamfer] Chamfer201  label="M3 Nut Smooth Hole084"
  Base = -> Groove079 [Edge24,Edge23]
  BaseFeature = -> Groove079
  Size = 0.2
FEATURE [PartDesign::Body] Body224  label="M3 Nut040"
  Group = -> [Sketch913,Pad367,Sketch907,Groove079,Chamfer201]
  Origin = -> Origin342
  Placement = pos=(-23,-9.8,62.05) rot=(0.57735,-0.57735,0.57735;2.0944rad)
  Tip = -> Chamfer201
FEATURE [Sketcher::SketchObject] Sketch916
  ExternalGeometry = -> [Pad365]
  MapMode = 5
  Placement = pos=(0,0,0) rot=(0.57735,0.57735,0.57735;2.0944rad)
  Support = -> [YZ_Plane306]
  sketch-geometry (6):
    g0: LineSegment StartX=-2.67543 StartY=1.2 StartZ=0 EndX=-3.67543 EndY=1.2 EndZ=0
    g1: LineSegment StartX=-3.67543 StartY=1.2 StartZ=0 EndX=-3.67543 EndY=-1.2 EndZ=0
    g2: LineSegment StartX=-3.67543 StartY=-1.2 StartZ=0 EndX=-2.67543 EndY=-1.2 EndZ=0
    g3: LineSegment StartX=-2.67543 StartY=-1.2 StartZ=0 EndX=-3.17543 EndY=-1 EndZ=0
    g4: LineSegment StartX=-3.17543 StartY=-1 StartZ=0 EndX=-3.17543 EndY=1 EndZ=0
    g5: LineSegment StartX=-3.17543 StartY=1 StartZ=0 EndX=-2.67543 EndY=1.2 EndZ=0
  constraints (15):
    c: Horizontal(g0)
    c: Coincident(g0,g1)
    c: Coincident(g1,g2)
    c: Coincident(g2,g3)
    c: Coincident(g3,g4)
    c: Coincident(g4,g5)
    c: Coincident(g5,g0)
    c: Symmetric(g4,g3,g-1)
    c: Symmetric(g0,g2,g-1)
    c: Symmetric(g1,g0,g-1)
    c: DistanceX(g0,g4) = 0.5
    c: DistanceY(g3,g4) = 2
    c: DistanceY(g1,g0) = 2.4
    c: PointOnObject(g3,g-3)
    c: DistanceX(g4,g0) = 0.5
FEATURE [PartDesign::Groove] Groove074  label="M3 Nut Smooth070"
  Angle = 360
  Axis = (-2e-16,3e-16,1)
  Base = (0,0,0)
  BaseFeature = -> Pad365
  Profile = -> Sketch916
  ReferenceAxis = -> Sketch916 [V_Axis]
  Reversed = true
FEATURE [PartDesign::Chamfer] Chamfer205  label="M3 Nut Smooth Hole086"
  Base = -> Groove074 [Edge24,Edge23]
  BaseFeature = -> Groove074
  Size = 0.2
FEATURE [PartDesign::Body] Body232  label="M3 Nut042"
  Group = -> [Sketch892,Pad365,Sketch916,Groove074,Chamfer205]
  Origin = -> Origin361
  Placement = pos=(-110.6,-9.3,52.1) rot=(0.57735,0.57735,-0.57735;2.0944rad)
  Tip = -> Chamfer205
FEATURE [App::Part] Part100  label="Shell Nuts001"
  Group = -> [Body192,Body196,Body228,Body232]
  Origin = -> Origin359
FEATURE [Sketcher::SketchObject] Sketch917
  MapMode = 5
  Support = -> [XY_Plane306]
  sketch-geometry (8):
    g0: LineSegment StartX=0 StartY=3.17543 StartZ=0 EndX=-2.75 EndY=1.58771 EndZ=0
    g1: LineSegment StartX=-2.75 StartY=1.58771 StartZ=0 EndX=-2.75 EndY=-1.58771 EndZ=0
    g2: LineSegment StartX=-2.75 StartY=-1.58771 StartZ=0 EndX=0 EndY=-3.17543 EndZ=0
    g3: LineSegment StartX=0 StartY=-3.17543 StartZ=0 EndX=2.75 EndY=-1.58771 EndZ=0
    g4: LineSegment StartX=2.75 StartY=-1.58771 StartZ=0 EndX=2.75 EndY=1.58771 EndZ=0
    g5: LineSegment StartX=2.75 StartY=1.58771 StartZ=0 EndX=0 EndY=3.17543 EndZ=0
    g6: Circle [constr] CenterX=0 CenterY=0 CenterZ=0 NormalX=0 NormalY=0 NormalZ=1 AngleXU=0 Radius=3.17543
    g7: Circle CenterX=0 CenterY=0 CenterZ=0 NormalX=0 NormalY=0 NormalZ=1 AngleXU=0 Radius=1.5
  constraints (18):
    c: Coincident(g0,g1)
    c: Coincident(g1,g2)
    c: Coincident(g2,g3)
    c: Coincident(g3,g4)
    c: Coincident(g4,g5)
    c: Coincident(g5,g0)
    c: Equal(g0, g1-g5) x5
    c: PointOnObject(g0,g6)
    c: PointOnObject(g1,g6)
    c: PointOnObject(g2,g6)
    c: PointOnObject(g3,g6)
    c: PointOnObject(g4,g6)
    c: PointOnObject(g5,g6)
    c: Coincident(g6,g-1)
    c: PointOnObject(g5,g-2)
    c: DistanceX(g0,g4) = 5.5
    c: Coincident(g7,g-1)
    c: Radius(g7) = 1.5
FEATURE [PartDesign::Pad] Pad368  label="M3 Nut Primitive072"
  Length = 1.2
  Length2 = 1.2
  Profile = -> Sketch917
  Type = 4
FEATURE [Sketcher::SketchObject] Sketch905
  ExternalGeometry = -> [Pad368]
  MapMode = 5
  Placement = pos=(0,0,0) rot=(0.57735,0.57735,0.57735;2.0944rad)
  Support = -> [YZ_Plane308]
  sketch-geometry (6):
    g0: LineSegment StartX=-2.67543 StartY=1.2 StartZ=0 EndX=-3.67543 EndY=1.2 EndZ=0
    g1: LineSegment StartX=-3.67543 StartY=1.2 StartZ=0 EndX=-3.67543 EndY=-1.2 EndZ=0
    g2: LineSegment StartX=-3.67543 StartY=-1.2 StartZ=0 EndX=-2.67543 EndY=-1.2 EndZ=0
    g3: LineSegment StartX=-2.67543 StartY=-1.2 StartZ=0 EndX=-3.17543 EndY=-1 EndZ=0
    g4: LineSegment StartX=-3.17543 StartY=-1 StartZ=0 EndX=-3.17543 EndY=1 EndZ=0
    g5: LineSegment StartX=-3.17543 StartY=1 StartZ=0 EndX=-2.67543 EndY=1.2 EndZ=0
  constraints (15):
    c: Horizontal(g0)
    c: Coincident(g0,g1)
    c: Coincident(g1,g2)
    c: Coincident(g2,g3)
    c: Coincident(g3,g4)
    c: Coincident(g4,g5)
    c: Coincident(g5,g0)
    c: Symmetric(g4,g3,g-1)
    c: Symmetric(g0,g2,g-1)
    c: Symmetric(g1,g0,g-1)
    c: DistanceX(g0,g4) = 0.5
    c: DistanceY(g3,g4) = 2
    c: DistanceY(g1,g0) = 2.4
    c: PointOnObject(g3,g-3)
    c: DistanceX(g4,g0) = 0.5
FEATURE [PartDesign::Groove] Groove075  label="M3 Nut Smooth071"
  Angle = 360
  Axis = (-2e-16,3e-16,1)
  Base = (0,0,0)
  BaseFeature = -> Pad368
  Profile = -> Sketch905
  ReferenceAxis = -> Sketch905 [V_Axis]
  Reversed = true
FEATURE [PartDesign::Chamfer] Chamfer202  label="M3 Nut Smooth Hole085"
  Base = -> Groove075 [Edge24,Edge23]
  BaseFeature = -> Groove075
  Size = 0.2
FEATURE [PartDesign::Body] Body211  label="M3 Nut037"
  Group = -> [Sketch917,Pad368,Sketch905,Groove075,Chamfer202]
  Origin = -> Origin367
  Placement = pos=(-23.1,-9.85,52.05) rot=(0.57735,-0.57735,0.57735;2.0944rad)
  Tip = -> Chamfer202
FEATURE [App::Part] Part106  label="Servo Nuts001"
  Group = -> [Body233,Body224,Body223,Body211]
  Origin = -> Origin330
FEATURE [Sketcher::SketchObject] Sketch920
  MapMode = 5
  Support = -> [XY_Plane327]
  sketch-geometry (1):
    g0: Circle CenterX=0 CenterY=10.15 CenterZ=0 NormalX=0 NormalY=0 NormalZ=1 AngleXU=0 Radius=3
  constraints (3):
    c: PointOnObject(g0,g-2)
    c: DistanceY(g-1,g0) = 10.15
    c: Radius(g0) = 3
FEATURE [PartDesign::Pad] Pad378
  Length = 5
  Length2 = 100
  Profile = -> Sketch920
  Type = 0
FEATURE [Sketcher::SketchObject] Sketch922
  ExternalGeometry = -> [Pad378]
  MapMode = 5
  Placement = pos=(0,0,5) rot=(0,0,1;0rad)
  Support = -> [Pad378]
  sketch-geometry (1):
    g0: Circle CenterX=0 CenterY=10.15 CenterZ=0 NormalX=0 NormalY=0 NormalZ=1 AngleXU=0 Radius=1.5
  constraints (2):
    c: Coincident(g0,g-3)
    c: Radius(g0) = 1.5
FEATURE [PartDesign::Pocket] Pocket378
  BaseFeature = -> Pad378
  Length = 4
  Length2 = 100
  Profile = -> Sketch922
  Type = 0
FEATURE [PartDesign::Chamfer] Chamfer203
  Base = -> Pocket378 [Edge3]
  BaseFeature = -> Pocket378
  Size = 0.25
FEATURE [PartDesign::Body] Body209  label="Gear007"
  Group = -> [Sketch920,Pad378,Sketch922,Pocket378,Chamfer203]
  Origin = -> Origin318
  Placement = pos=(0,0,38.25) rot=(0,0,1;0rad)
  Tip = -> Chamfer203
FEATURE [Sketcher::SketchObject] Sketch923
  MapMode = 5
  Placement = pos=(0,0,0) rot=(1,0,0;1.5708rad)
  Support = -> [XZ_Plane324]
  sketch-geometry (1):
    g0: Circle CenterX=-1.55 CenterY=4 CenterZ=0 NormalX=0 NormalY=0 NormalZ=1 AngleXU=0 Radius=0.75
  constraints (3):
    c: Radius(g0) = 0.75
    c: DistanceY(g-1,g0) = 4
    c: DistanceX(g0,g-1) = 1.55
FEATURE [PartDesign::Pad] Pad388
  Length = 10
  Length2 = 100
  Placement = pos=(0,0,0) rot=(1,0,0;1.5708rad)
  Profile = -> Sketch923
  Reversed = true
  Type = 0
FEATURE [PartDesign::Body] Body210  label="orange wire006"
  Group = -> [Sketch923,Pad388]
  Origin = -> Origin351
  Placement = pos=(0,25.15,0) rot=(0,0,1;0rad)
  Tip = -> Pad388
FEATURE [Sketcher::SketchObject] Sketch924
  MapMode = 5
  Support = -> [XY_Plane337]
  sketch-geometry (1):
    g0: Circle CenterX=0 CenterY=0 CenterZ=0 NormalX=0 NormalY=0 NormalZ=1 AngleXU=0 Radius=2.75
  constraints (2):
    c: Coincident(g0,g-1)
    c: Radius(g0) = 2.75
FEATURE [PartDesign::Pad] Pad387  label="M3x20 Head028"
  Length = 3
  Length2 = 100
  Profile = -> Sketch924
  Type = 0
FEATURE [Sketcher::SketchObject] Sketch926
  MapMode = 5
  Support = -> [XY_Plane321]
  sketch-geometry (4):
    g0: LineSegment StartX=-10 StartY=20.15 StartZ=0 EndX=10 EndY=20.15 EndZ=0
    g1: LineSegment StartX=10 StartY=20.15 StartZ=0 EndX=10 EndY=-20.15 EndZ=0
    g2: LineSegment StartX=10 StartY=-20.15 StartZ=0 EndX=-10 EndY=-20.15 EndZ=0
    g3: LineSegment StartX=-10 StartY=-20.15 StartZ=0 EndX=-10 EndY=20.15 EndZ=0
  constraints (10):
    c: Coincident(g0,g1)
    c: Coincident(g1,g2)
    c: Coincident(g2,g3)
    c: Coincident(g3,g0)
    c: Horizontal(g2)
    c: Vertical(g3)
    c: DistanceX(g0,g0) = 20
    c: DistanceY(g1,g1) = 40.3
    c: Symmetric(g0,g1,g-1)
    c: Symmetric(g0,g0,g-2)
FEATURE [PartDesign::Pad] Pad372  label="Baseblock008"
  Length = 26.6
  Length2 = 100
  Profile = -> Sketch926
  Type = 0
FEATURE [Sketcher::SketchObject] Sketch895
  MapMode = 5
  Placement = pos=(0,0,26.6) rot=(0,0,1;0rad)
  Support = -> [Pad372]
  sketch-geometry (4):
    g0: LineSegment StartX=-10 StartY=-26.8 StartZ=0 EndX=10 EndY=-26.8 EndZ=0
    g1: LineSegment StartX=10 StartY=-26.8 StartZ=0 EndX=10 EndY=26.8 EndZ=0
    g2: LineSegment StartX=10 StartY=26.8 StartZ=0 EndX=-10 EndY=26.8 EndZ=0
    g3: LineSegment StartX=-10 StartY=26.8 StartZ=0 EndX=-10 EndY=-26.8 EndZ=0
  constraints (10):
    c: Coincident(g0,g1)
    c: Coincident(g1,g2)
    c: Coincident(g2,g3)
    c: Coincident(g3,g0)
    c: Horizontal(g0)
    c: Vertical(g3)
    c: Symmetric(g1,g2,g-2)
    c: Symmetric(g1,g0,g-1)
    c: DistanceX(g2,g2) = 20
    c: DistanceY(g1,g1) = 53.6
FEATURE [PartDesign::Pad] Pad377
  BaseFeature = -> Pad372
  Length = 2.5
  Length2 = 100
  Profile = -> Sketch895
  Type = 0
FEATURE [Sketcher::SketchObject] Sketch914
  MapMode = 5
  Placement = pos=(0,0,29.1) rot=(0,0,1;0rad)
  Support = -> [Pad377]
  sketch-geometry (4):
    g0: LineSegment StartX=-10 StartY=-20.15 StartZ=0 EndX=10 EndY=-20.15 EndZ=0
    g1: LineSegment StartX=10 StartY=-20.15 StartZ=0 EndX=10 EndY=20.15 EndZ=0
    g2: LineSegment StartX=10 StartY=20.15 StartZ=0 EndX=-10 EndY=20.15 EndZ=0
    g3: LineSegment StartX=-10 StartY=20.15 StartZ=0 EndX=-10 EndY=-20.15 EndZ=0
  constraints (10):
    c: Coincident(g0,g1)
    c: Coincident(g1,g2)
    c: Coincident(g2,g3)
    c: Coincident(g3,g0)
    c: Horizontal(g0)
    c: Vertical(g3)
    c: Symmetric(g1,g2,g-2)
    c: Symmetric(g1,g0,g-1)
    c: DistanceX(g2,g2) = 20
    c: DistanceY(g1,g1) = 40.3
FEATURE [PartDesign::Pad] Pad374
  BaseFeature = -> Pad377
  Length = 6
  Length2 = 100
  Profile = -> Sketch914
  Type = 0
FEATURE [Sketcher::SketchObject] Sketch928
  MapMode = 5
  Support = -> [XY_Plane342]
  sketch-geometry (1):
    g0: Circle CenterX=0 CenterY=0 CenterZ=0 NormalX=0 NormalY=0 NormalZ=1 AngleXU=0 Radius=2.75
  constraints (2):
    c: Coincident(g0,g-1)
    c: Radius(g0) = 2.75
FEATURE [PartDesign::Pad] Pad390  label="M3x20 Head030"
  Length = 3
  Length2 = 100
  Profile = -> Sketch928
  Type = 0
FEATURE [Sketcher::SketchObject] Sketch931
  ExternalGeometry = -> [Pad374]
  MapMode = 5
  Placement = pos=(0,0,35.1) rot=(0,0,1;0rad)
  Support = -> [Pad374]
  sketch-geometry (7):
    g0: ArcOfCircle CenterX=-3e-16 CenterY=10.15 CenterZ=0 NormalX=0 NormalY=0 NormalZ=1 AngleXU=0 Radius=9.5 StartAngle=5.9573 EndAngle=9.75066
    g1: LineSegment StartX=-9 StartY=7.10862 StartZ=0 EndX=-9 EndY=-14.15 EndZ=0
    g2: LineSegment StartX=-9 StartY=-14.15 StartZ=0 EndX=-5 EndY=-14.15 EndZ=0
    g3: LineSegment StartX=5 StartY=-14.15 StartZ=0 EndX=9 EndY=-14.15 EndZ=0
    g4: LineSegment StartX=9 StartY=-14.15 StartZ=0 EndX=9 EndY=7.10862 EndZ=0
    g5: ArcOfCircle CenterX=-3e-16 CenterY=-10.4 CenterZ=0 NormalX=0 NormalY=0 NormalZ=1 AngleXU=0 Radius=6.25 StartAngle=3.78509 EndAngle=5.63968
    g6: LineSegment [constr] StartX=0 StartY=-20.15 StartZ=0 EndX=0 EndY=-16.65 EndZ=0
  constraints (22):
    c: Symmetric(g0,g0,g-2)
    c: Coincident(g1,g0)
    c: Vertical(g1)
    c: Coincident(g2,g1)
    c: Horizontal(g2)
    c: Horizontal(g3)
    c: Coincident(g4,g3)
    c: Coincident(g4,g0)
    c: Vertical(g4)
    c: Symmetric(g2,g3,g-2)
    c: Coincident(g5,g2)
    c: Coincident(g5,g3)
    c: DistanceY(g-3,g3) = 6
    c: DistanceY(g0,g-4) = 10
    c: Radius(g0) = 9.5
    c: DistanceX(g0,g0) = 18
    c: PointOnObject(g6,g-3)
    c: PointOnObject(g6,g5)
    c: Vertical(g6)
    c: DistanceY(g6,g6) = 3.5
    c: DistanceX(g2,g3) = 10
    c: PointOnObject(g6,g-2)
FEATURE [PartDesign::Pad] Pad376
  BaseFeature = -> Pad374
  Length = 2.5
  Length2 = 100
  Profile = -> Sketch931
  Type = 0
FEATURE [Sketcher::SketchObject] Sketch912
  ExternalGeometry = -> [Pad376]
  MapMode = 5
  Placement = pos=(0,0,37.6) rot=(0,0,1;0rad)
  Support = -> [Pad376]
  sketch-geometry (1):
    g0: Circle CenterX=-3e-16 CenterY=10.15 CenterZ=0 NormalX=0 NormalY=0 NormalZ=1 AngleXU=0 Radius=6.5
  constraints (2):
    c: Coincident(g0,g-3)
    c: Radius(g0) = 6.5
FEATURE [PartDesign::Pad] Pad385
  BaseFeature = -> Pad376
  Length = 1
  Length2 = 100
  Profile = -> Sketch912
  Type = 0
FEATURE [Sketcher::SketchObject] Sketch908
  ExternalGeometry = -> [Pad385]
  MapMode = 5
  Placement = pos=(0,0,38.6) rot=(0,0,1;0rad)
  Support = -> [Pad385]
  sketch-geometry (1):
    g0: Circle CenterX=0 CenterY=10.15 CenterZ=0 NormalX=0 NormalY=0 NormalZ=1 AngleXU=0 Radius=5.5
  constraints (2):
    c: Coincident(g0,g-3)
    c: Radius(g0) = 5.5
FEATURE [PartDesign::Pad] Pad386
  BaseFeature = -> Pad385
  Length = 0.5
  Length2 = 100
  Profile = -> Sketch908
  Type = 0
FEATURE [Sketcher::SketchObject] Sketch932
  MapMode = 5
  Placement = pos=(0,0,0) rot=(1,0,0;1.5708rad)
  Support = -> [XZ_Plane320]
  sketch-geometry (1):
    g0: Circle CenterX=0 CenterY=4 CenterZ=0 NormalX=0 NormalY=0 NormalZ=1 AngleXU=0 Radius=0.75
  constraints (3):
    c: PointOnObject(g0,g-2)
    c: Radius(g0) = 0.75
    c: DistanceY(g-1,g0) = 4
FEATURE [PartDesign::Pad] Pad379
  Length = 10
  Length2 = 100
  Placement = pos=(0,0,0) rot=(1,0,0;1.5708rad)
  Profile = -> Sketch932
  Reversed = true
  Type = 0
FEATURE [PartDesign::Body] Body194  label="red wire007"
  Group = -> [Sketch932,Pad379]
  Origin = -> Origin352
  Placement = pos=(0,25.15,0) rot=(0,0,1;0rad)
  Tip = -> Pad379
FEATURE [Sketcher::SketchObject] Sketch935
  ExternalGeometry = -> [Pad386]
  MapMode = 5
  Placement = pos=(0,0,39.1) rot=(0,0,1;0rad)
  Support = -> [Pad386]
  sketch-geometry (1):
    g0: Circle CenterX=0 CenterY=10.15 CenterZ=0 NormalX=0 NormalY=0 NormalZ=1 AngleXU=0 Radius=3
  constraints (2):
    c: Coincident(g0,g-3)
    c: Radius(g0) = 3
FEATURE [PartDesign::Pad] Pad373
  BaseFeature = -> Pad386
  Length = 4
  Length2 = 100
  Profile = -> Sketch935
  Type = 0
FEATURE [Sketcher::SketchObject] Sketch929
  ExternalGeometry = -> [Pad373]
  MapMode = 5
  Placement = pos=(0,0,43.1) rot=(0,0,1;0rad)
  Support = -> [Pad373]
  sketch-geometry (1):
    g0: Circle CenterX=0 CenterY=10.15 CenterZ=0 NormalX=0 NormalY=0 NormalZ=1 AngleXU=0 Radius=1.5
  constraints (2):
    c: Coincident(g0,g-3)
    c: Radius(g0) = 1.5
FEATURE [PartDesign::Pocket] Pocket382
  BaseFeature = -> Pad373
  Length = 5
  Length2 = 100
  Profile = -> Sketch929
  Type = 0
FEATURE [Sketcher::SketchObject] Sketch919
  MapMode = 5
  Placement = pos=(0,0,29.1) rot=(0,0,1;0rad)
  Support = -> [Pocket382]
  sketch-geometry (4):
    g0: Circle CenterX=-4.91157 CenterY=25.3 CenterZ=0 NormalX=0 NormalY=0 NormalZ=1 AngleXU=0 Radius=2.25
    g1: Circle CenterX=4.91157 CenterY=25.3 CenterZ=0 NormalX=0 NormalY=0 NormalZ=1 AngleXU=0 Radius=2.25
    g2: Circle CenterX=-4.91157 CenterY=-25.3 CenterZ=0 NormalX=0 NormalY=0 NormalZ=1 AngleXU=0 Radius=2.25
    g3: Circle CenterX=4.91157 CenterY=-25.3 CenterZ=0 NormalX=0 NormalY=0 NormalZ=1 AngleXU=0 Radius=2.25
  constraints (8):
    c: Equal(g3,g2)
    c: Equal(g2,g1)
    c: Equal(g1,g0)
    c: Radius(g1) = 2.25
    c: Symmetric(g1,g0,g-2)
    c: Symmetric(g3,g2,g-2)
    c: Symmetric(g3,g1,g-1)
    c: DistanceY(g3,g1) = 50.6
FEATURE [PartDesign::Pocket] Pocket369
  BaseFeature = -> Pocket382
  Length = 5
  Length2 = 100
  Profile = -> Sketch919
  Type = 0
FEATURE [Sketcher::SketchObject] Sketch915
  MapMode = 5
  Placement = pos=(0,0,29.1) rot=(0,0,1;0rad)
  Support = -> [Pocket369]
  sketch-geometry (8):
    g0: LineSegment StartX=-0.5 StartY=26.8 StartZ=0 EndX=0.5 EndY=26.8 EndZ=0
    g1: LineSegment StartX=0.5 StartY=26.8 StartZ=0 EndX=0.5 EndY=20.15 EndZ=0
    g2: LineSegment StartX=0.5 StartY=20.15 StartZ=0 EndX=-0.5 EndY=20.15 EndZ=0
    g3: LineSegment StartX=-0.5 StartY=20.15 StartZ=0 EndX=-0.5 EndY=26.8 EndZ=0
    g4: LineSegment StartX=-0.5 StartY=-20.15 StartZ=0 EndX=0.5 EndY=-20.15 EndZ=0
    g5: LineSegment StartX=0.5 StartY=-20.15 StartZ=0 EndX=0.5 EndY=-26.8 EndZ=0
    g6: LineSegment StartX=0.5 StartY=-26.8 StartZ=0 EndX=-0.5 EndY=-26.8 EndZ=0
    g7: LineSegment StartX=-0.5 StartY=-26.8 StartZ=0 EndX=-0.5 EndY=-20.15 EndZ=0
  constraints (20):
    c: Coincident(g0,g1)
    c: Coincident(g1,g2)
    c: Coincident(g2,g3)
    c: Coincident(g3,g0)
    c: Horizontal(g2)
    c: Vertical(g1)
    c: Vertical(g3)
    c: Coincident(g4,g5)
    c: Coincident(g5,g6)
    c: Coincident(g6,g7)
    c: Coincident(g7,g4)
    c: Horizontal(g6)
    c: Vertical(g7)
    c: Symmetric(g4,g4,g-2)
    c: Symmetric(g0,g0,g-2)
    c: Symmetric(g0,g5,g-1)
    c: DistanceY(g5,g0) = 53.6
    c: DistanceY(g4,g1) = 40.3
    c: DistanceX(g0,g0) = 1
    c: Symmetric(g4,g1,g-1)
FEATURE [PartDesign::Pad] Pad381
  BaseFeature = -> Pocket369
  Length = 2
  Length2 = 100
  Profile = -> Sketch915
  Type = 0
FEATURE [Sketcher::SketchObject] Sketch927
  ExternalGeometry = -> [Pad381]
  MapMode = 5
  Placement = pos=(0.5,0,0) rot=(0.57735,0.57735,0.57735;2.0944rad)
  Support = -> [Pad381]
  sketch-geometry (6):
    g0: LineSegment StartX=-26.8 StartY=29.1 StartZ=0 EndX=-26.8 EndY=31.1 EndZ=0
    g1: LineSegment StartX=-26.8 StartY=31.1 StartZ=0 EndX=-20.15 EndY=31.1 EndZ=0
    g2: LineSegment StartX=-20.15 StartY=31.1 StartZ=0 EndX=-26.8 EndY=29.1 EndZ=0
    g3: LineSegment StartX=20.15 StartY=31.1 StartZ=0 EndX=26.8 EndY=31.1 EndZ=0
    g4: LineSegment StartX=26.8 StartY=31.1 StartZ=0 EndX=26.8 EndY=29.1 EndZ=0
    g5: LineSegment StartX=26.8 StartY=29.1 StartZ=0 EndX=20.15 EndY=31.1 EndZ=0
  constraints (14):
    c: Vertical(g0)
    c: Coincident(g0,g1)
    c: Horizontal(g1)
    c: Coincident(g1,g2)
    c: Coincident(g2,g0)
    c: Coincident(g3,g4)
    c: Coincident(g4,g5)
    c: Coincident(g5,g3)
    c: Symmetric(g0,g4,g-2)
    c: Symmetric(g3,g0,g-2)
    c: Symmetric(g1,g3,g-2)
    c: DistanceX(g0,g3) = 53.6
    c: DistanceY(g4,g4) = 2
    c: Coincident(g3,g-3)
FEATURE [PartDesign::Pocket] Pocket383
  BaseFeature = -> Pad381
  Length = 1
  Length2 = 100
  Profile = -> Sketch927
  Type = 0
FEATURE [PartDesign::Fillet] Fillet118
  Base = -> Pocket383 [Edge26,Edge27,Edge72,Edge63,Edge70,Edge78,Edge51,Edge49,Edge71,Edge50,Edge79,Edge86,Edge30,Edge21,Edge4,Edge29,Edge105,Edge107,Edge109,Edge111,Edge113,Edge114,Edge123]
  BaseFeature = -> Pocket383
  Radius = 0.4
FEATURE [Sketcher::SketchObject] Sketch930
  MapMode = 5
  Placement = pos=(0,20.15,0) rot=(0,0.707107,0.707107;3.14159rad)
  Support = -> [Fillet118]
  sketch-geometry (4):
    g0: LineSegment StartX=-3.25 StartY=2 StartZ=0 EndX=3.25 EndY=2 EndZ=0
    g1: LineSegment StartX=3.25 StartY=2 StartZ=0 EndX=3.25 EndY=6 EndZ=0
    g2: LineSegment StartX=3.25 StartY=6 StartZ=0 EndX=-3.25 EndY=6 EndZ=0
    g3: LineSegment StartX=-3.25 StartY=6 StartZ=0 EndX=-3.25 EndY=2 EndZ=0
  constraints (11):
    c: Coincident(g0,g1)
    c: Coincident(g1,g2)
    c: Coincident(g2,g3)
    c: Coincident(g3,g0)
    c: Horizontal(g0)
    c: Vertical(g1)
    c: Vertical(g3)
    c: DistanceY(g-1,g0) = 2
    c: DistanceY(g1,g1) = 4
    c: Symmetric(g2,g1,g-2)
    c: DistanceX(g2,g2) = 6.5
FEATURE [PartDesign::Pad] Pad364
  BaseFeature = -> Fillet118
  Length = 1
  Length2 = 100
  Profile = -> Sketch930
  Type = 0
FEATURE [Sketcher::SketchObject] Sketch921
  MapMode = 5
  Placement = pos=(0,21.15,0) rot=(0,0.707107,0.707107;3.14159rad)
  Support = -> [Pad364]
  sketch-geometry (4):
    g0: LineSegment StartX=-2.75 StartY=5.5 StartZ=0 EndX=2.75 EndY=5.5 EndZ=0
    g1: LineSegment StartX=2.75 StartY=5.5 StartZ=0 EndX=2.75 EndY=2.5 EndZ=0
    g2: LineSegment StartX=2.75 StartY=2.5 StartZ=0 EndX=-2.75 EndY=2.5 EndZ=0
    g3: LineSegment StartX=-2.75 StartY=2.5 StartZ=0 EndX=-2.75 EndY=5.5 EndZ=0
  constraints (11):
    c: Coincident(g0,g1)
    c: Coincident(g1,g2)
    c: Coincident(g2,g3)
    c: Coincident(g3,g0)
    c: Horizontal(g0)
    c: Vertical(g1)
    c: Vertical(g3)
    c: Symmetric(g1,g2,g-2)
    c: DistanceY(g1,g0) = 3
    c: DistanceY(g-1,g1) = 2.5
    c: DistanceX(g0,g0) = 5.5
FEATURE [PartDesign::Pad] Pad382
  BaseFeature = -> Pad364
  Length = 4
  Length2 = 100
  Profile = -> Sketch921
  Type = 0
FEATURE [Sketcher::SketchObject] Sketch906
  MapMode = 5
  Placement = pos=(0,0,0) rot=(1,0,0;3.14159rad)
  Support = -> [Pad382]
  sketch-geometry (4):
    g0: LineSegment StartX=-10 StartY=-20.15 StartZ=0 EndX=10 EndY=-20.15 EndZ=0
    g1: LineSegment StartX=10 StartY=-20.15 StartZ=0 EndX=10 EndY=20.15 EndZ=0
    g2: LineSegment StartX=10 StartY=20.15 StartZ=0 EndX=-10 EndY=20.15 EndZ=0
    g3: LineSegment StartX=-10 StartY=20.15 StartZ=0 EndX=-10 EndY=-20.15 EndZ=0
  constraints (10):
    c: Coincident(g0,g1)
    c: Coincident(g1,g2)
    c: Coincident(g2,g3)
    c: Coincident(g3,g0)
    c: Horizontal(g0)
    c: Vertical(g1)
    c: Symmetric(g2,g1,g-2)
    c: Symmetric(g0,g2,g-1)
    c: DistanceX(g2,g2) = 20
    c: DistanceY(g1,g1) = 40.3
FEATURE [PartDesign::Pad] Pad380
  BaseFeature = -> Pad382
  Length = 2
  Length2 = 100
  Profile = -> Sketch906
  Type = 0
FEATURE [PartDesign::Chamfer] Chamfer196
  Base = -> Pad380 [Face7]
  BaseFeature = -> Pad380
  Size = 1.5
FEATURE [PartDesign::Fillet] Fillet117
  Base = -> Chamfer196 [Edge1,Edge7,Edge18,Edge4,Face12]
  BaseFeature = -> Chamfer196
  Radius = 0.4
FEATURE [Sketcher::SketchObject] Sketch918
  ExternalGeometry = -> [Fillet117]
  MapMode = 5
  Placement = pos=(0,0,43.1) rot=(0,0,1;0rad)
  Support = -> [Fillet117]
  sketch-geometry (1):
    g0: Circle CenterX=0 CenterY=10.15 CenterZ=0 NormalX=0 NormalY=0 NormalZ=1 AngleXU=0 Radius=3
  constraints (2):
    c: Coincident(g0,g-3)
    c: Radius(g0) = 3
FEATURE [PartDesign::Pocket] Pocket370
  BaseFeature = -> Fillet117
  Length = 5
  Length2 = 100
  Profile = -> Sketch918
  Type = 0
FEATURE [PartDesign::Body] Body188  label="MG996R005"
  Group = -> [Sketch926,Pad372,Sketch895,Pad377,Sketch914,Pad374,Sketch931,Pad376,Sketch912,Pad385,Sketch908,Pad386,Sketch935,Pad373,Sketch929,Pocket382,Sketch919,Pocket369,Sketch915,Pad381,Sketch927,Pocket383,Fillet118,Sketch930,Pad364,Sketch921,Pad382,Sketch906,Pad380,Chamfer196,Fillet117,Sketch918,Pocket370]
  Origin = -> Origin319
  Tip = -> Pocket370
FEATURE [App::Part] Part101  label="Servo006"
  Group = -> [Body188,Body209,Body194,Body210,Body191]
  Origin = -> Origin340
  Placement = pos=(-47.3841,6.65,56.9914) rot=(-0.57735,-0.57735,0.57735;4.18879rad)
FEATURE [Sketcher::SketchObject] Sketch936
  MapMode = 5
  Placement = pos=(0,0,3) rot=(0,0,1;0rad)
  Support = -> [Pad390]
  sketch-geometry (1):
    g0: Circle CenterX=0 CenterY=0 CenterZ=0 NormalX=0 NormalY=0 NormalZ=1 AngleXU=0 Radius=1.5
  constraints (2):
    c: Coincident(g0,g-1)
    c: Radius(g0) = 1.5
FEATURE [PartDesign::Pad] Pad375  label="M3x20 Thread028"
  BaseFeature = -> Pad390
  Length = 20
  Length2 = 100
  Profile = -> Sketch936
  Type = 0
FEATURE [Sketcher::SketchObject] Sketch934
  MapMode = 5
  Placement = pos=(0,0,0) rot=(1,0,0;3.14159rad)
  Support = -> [Pad375]
  sketch-geometry (7):
    g0: LineSegment StartX=1.275 StartY=0.736122 StartZ=0 EndX=0 EndY=1.47224 EndZ=0
    g1: LineSegment StartX=0 StartY=1.47224 StartZ=0 EndX=-1.275 EndY=0.736122 EndZ=0
    g2: LineSegment StartX=-1.275 StartY=0.736122 StartZ=0 EndX=-1.275 EndY=-0.736122 EndZ=0
    g3: LineSegment StartX=-1.275 StartY=-0.736122 StartZ=0 EndX=1.34766e-11 EndY=-1.47224 EndZ=0
    g4: LineSegment StartX=1.34766e-11 StartY=-1.47224 StartZ=0 EndX=1.275 EndY=-0.736122 EndZ=0
    g5: LineSegment StartX=1.275 StartY=-0.736122 StartZ=0 EndX=1.275 EndY=0.736122 EndZ=0
    g6: Circle [constr] CenterX=0 CenterY=0 CenterZ=0 NormalX=0 NormalY=0 NormalZ=1 AngleXU=0 Radius=1.47224
  constraints (16):
    c: Coincident(g0,g1)
    c: Coincident(g1,g2)
    c: Coincident(g2,g3)
    c: Coincident(g3,g4)
    c: Coincident(g4,g5)
    c: Coincident(g5,g0)
    c: Equal(g0, g1-g5) x5
    c: PointOnObject(g0,g6)
    c: PointOnObject(g1,g6)
    c: PointOnObject(g2,g6)
    c: PointOnObject(g3,g6)
    c: PointOnObject(g4,g6)
    c: PointOnObject(g5,g6)
    c: Coincident(g6,g-1)
    c: PointOnObject(g0,g-2)
    c: DistanceX(g1,g0) = 2.55
FEATURE [PartDesign::Pocket] Pocket367  label="M3x20 Wrench028"
  BaseFeature = -> Pad375
  Length = 1.3
  Length2 = 100
  Profile = -> Sketch934
  Type = 0
FEATURE [PartDesign::Chamfer] Chamfer204  label="M3x20 Smooth035"
  Base = -> Pocket367 [Face11,Edge2,Edge24,Edge3]
  BaseFeature = -> Pocket367
  Size = 0.2
FEATURE [PartDesign::Body] Body218  label="M3x050"
  Group = -> [Sketch928,Pad390,Sketch936,Pad375,Sketch934,Pocket367,Chamfer204]
  Origin = -> Origin321
  Placement = pos=(-115.35,-29.35,62.05) rot=(-1,0,0;1.5708rad)
  Tip = -> Chamfer204
FEATURE [Sketcher::SketchObject] Sketch939
  MapMode = 5
  Support = -> [XY_Plane319]
  sketch-geometry (1):
    g0: Circle CenterX=0 CenterY=0 CenterZ=0 NormalX=0 NormalY=0 NormalZ=1 AngleXU=0 Radius=2.75
  constraints (2):
    c: Coincident(g0,g-1)
    c: Radius(g0) = 2.75
FEATURE [PartDesign::Pad] Pad389  label="M3x20 Head029"
  Length = 3
  Length2 = 100
  Profile = -> Sketch939
  Type = 0
FEATURE [Sketcher::SketchObject] Sketch940
  MapMode = 5
  Placement = pos=(0,0,3) rot=(0,0,1;0rad)
  Support = -> [Pad389]
  sketch-geometry (1):
    g0: Circle CenterX=0 CenterY=0 CenterZ=0 NormalX=0 NormalY=0 NormalZ=1 AngleXU=0 Radius=1.5
  constraints (2):
    c: Coincident(g0,g-1)
    c: Radius(g0) = 1.5
FEATURE [PartDesign::Pad] Pad392  label="M3x20 Thread029"
  BaseFeature = -> Pad389
  Length = 20
  Length2 = 100
  Profile = -> Sketch940
  Type = 0
FEATURE [Sketcher::SketchObject] Sketch941
  MapMode = 5
  Placement = pos=(0,0,3) rot=(0,0,1;0rad)
  Support = -> [Pad387]
  sketch-geometry (1):
    g0: Circle CenterX=0 CenterY=0 CenterZ=0 NormalX=0 NormalY=0 NormalZ=1 AngleXU=0 Radius=1.5
  constraints (2):
    c: Coincident(g0,g-1)
    c: Radius(g0) = 1.5
FEATURE [PartDesign::Pad] Pad401  label="M3x20 Thread034"
  BaseFeature = -> Pad387
  Length = 20
  Length2 = 100
  Profile = -> Sketch941
  Type = 0
FEATURE [Sketcher::SketchObject] Sketch938
  MapMode = 5
  Placement = pos=(0,0,0) rot=(1,0,0;3.14159rad)
  Support = -> [Pad401]
  sketch-geometry (7):
    g0: LineSegment StartX=1.275 StartY=0.736122 StartZ=0 EndX=0 EndY=1.47224 EndZ=0
    g1: LineSegment StartX=0 StartY=1.47224 StartZ=0 EndX=-1.275 EndY=0.736122 EndZ=0
    g2: LineSegment StartX=-1.275 StartY=0.736122 StartZ=0 EndX=-1.275 EndY=-0.736122 EndZ=0
    g3: LineSegment StartX=-1.275 StartY=-0.736122 StartZ=0 EndX=1.34766e-11 EndY=-1.47224 EndZ=0
    g4: LineSegment StartX=1.34766e-11 StartY=-1.47224 StartZ=0 EndX=1.275 EndY=-0.736122 EndZ=0
    g5: LineSegment StartX=1.275 StartY=-0.736122 StartZ=0 EndX=1.275 EndY=0.736122 EndZ=0
    g6: Circle [constr] CenterX=0 CenterY=0 CenterZ=0 NormalX=0 NormalY=0 NormalZ=1 AngleXU=0 Radius=1.47224
  constraints (16):
    c: Coincident(g0,g1)
    c: Coincident(g1,g2)
    c: Coincident(g2,g3)
    c: Coincident(g3,g4)
    c: Coincident(g4,g5)
    c: Coincident(g5,g0)
    c: Equal(g0, g1-g5) x5
    c: PointOnObject(g0,g6)
    c: PointOnObject(g1,g6)
    c: PointOnObject(g2,g6)
    c: PointOnObject(g3,g6)
    c: PointOnObject(g4,g6)
    c: PointOnObject(g5,g6)
    c: Coincident(g6,g-1)
    c: PointOnObject(g0,g-2)
    c: DistanceX(g1,g0) = 2.55
FEATURE [Sketcher::SketchObject] Sketch943
  MapMode = 5
  Support = -> [XY_Plane330]
  sketch-geometry (1):
    g0: Circle CenterX=0 CenterY=0 CenterZ=0 NormalX=0 NormalY=0 NormalZ=1 AngleXU=0 Radius=2.75
  constraints (2):
    c: Coincident(g0,g-1)
    c: Radius(g0) = 2.75
FEATURE [PartDesign::Pad] Pad391  label="M3x20 Head031"
  Length = 3
  Length2 = 100
  Profile = -> Sketch943
  Type = 0
FEATURE [Sketcher::SketchObject] Sketch945
  MapMode = 5
  Support = -> [XY_Plane324]
  sketch-geometry (1):
    g0: Circle CenterX=0 CenterY=0 CenterZ=0 NormalX=0 NormalY=0 NormalZ=1 AngleXU=0 Radius=2.75
  constraints (2):
    c: Coincident(g0,g-1)
    c: Radius(g0) = 2.75
FEATURE [Sketcher::SketchObject] Sketch946
  MapMode = 5
  Support = -> [XY_Plane336]
  sketch-geometry (1):
    g0: Circle CenterX=0 CenterY=0 CenterZ=0 NormalX=0 NormalY=0 NormalZ=1 AngleXU=0 Radius=2.75
  constraints (2):
    c: Coincident(g0,g-1)
    c: Radius(g0) = 2.75
FEATURE [PartDesign::Pad] Pad393  label="M3x20 Head032"
  Length = 3
  Length2 = 100
  Profile = -> Sketch946
  Type = 0
FEATURE [Sketcher::SketchObject] Sketch933
  MapMode = 5
  Placement = pos=(0,0,3) rot=(0,0,1;0rad)
  Support = -> [Pad393]
  sketch-geometry (1):
    g0: Circle CenterX=0 CenterY=0 CenterZ=0 NormalX=0 NormalY=0 NormalZ=1 AngleXU=0 Radius=1.5
  constraints (2):
    c: Coincident(g0,g-1)
    c: Radius(g0) = 1.5
FEATURE [PartDesign::Pad] Pad399  label="M3x20 Thread033"
  BaseFeature = -> Pad393
  Length = 20
  Length2 = 100
  Profile = -> Sketch933
  Type = 0
FEATURE [Sketcher::SketchObject] Sketch944
  MapMode = 5
  Placement = pos=(0,0,0) rot=(1,0,0;3.14159rad)
  Support = -> [Pad399]
  sketch-geometry (7):
    g0: LineSegment StartX=1.275 StartY=0.736122 StartZ=0 EndX=0 EndY=1.47224 EndZ=0
    g1: LineSegment StartX=0 StartY=1.47224 StartZ=0 EndX=-1.275 EndY=0.736122 EndZ=0
    g2: LineSegment StartX=-1.275 StartY=0.736122 StartZ=0 EndX=-1.275 EndY=-0.736122 EndZ=0
    g3: LineSegment StartX=-1.275 StartY=-0.736122 StartZ=0 EndX=1.34766e-11 EndY=-1.47224 EndZ=0
    g4: LineSegment StartX=1.34766e-11 StartY=-1.47224 StartZ=0 EndX=1.275 EndY=-0.736122 EndZ=0
    g5: LineSegment StartX=1.275 StartY=-0.736122 StartZ=0 EndX=1.275 EndY=0.736122 EndZ=0
    g6: Circle [constr] CenterX=0 CenterY=0 CenterZ=0 NormalX=0 NormalY=0 NormalZ=1 AngleXU=0 Radius=1.47224
  constraints (16):
    c: Coincident(g0,g1)
    c: Coincident(g1,g2)
    c: Coincident(g2,g3)
    c: Coincident(g3,g4)
    c: Coincident(g4,g5)
    c: Coincident(g5,g0)
    c: Equal(g0, g1-g5) x5
    c: PointOnObject(g0,g6)
    c: PointOnObject(g1,g6)
    c: PointOnObject(g2,g6)
    c: PointOnObject(g3,g6)
    c: PointOnObject(g4,g6)
    c: PointOnObject(g5,g6)
    c: Coincident(g6,g-1)
    c: PointOnObject(g0,g-2)
    c: DistanceX(g1,g0) = 2.55
FEATURE [PartDesign::Pocket] Pocket377  label="M3x20 Wrench032"
  BaseFeature = -> Pad399
  Length = 1.3
  Length2 = 100
  Profile = -> Sketch944
  Type = 0
FEATURE [PartDesign::Chamfer] Chamfer149  label="M3x20 Smooth029"
  Base = -> Pocket377 [Face11,Edge2,Edge24,Edge3]
  BaseFeature = -> Pocket377
  Size = 0.2
FEATURE [PartDesign::Body] Body197  label="M3x042"
  Group = -> [Sketch946,Pad393,Sketch933,Pad399,Sketch944,Pocket377,Chamfer149]
  Origin = -> Origin264
  Placement = pos=(-23,-25.6,62.05) rot=(-1,0,0;1.5708rad)
  Tip = -> Chamfer149
FEATURE [Sketcher::SketchObject] Sketch948
  MapMode = 5
  Support = -> [XY_Plane341]
  sketch-geometry (1):
    g0: Circle CenterX=0 CenterY=0 CenterZ=0 NormalX=0 NormalY=0 NormalZ=1 AngleXU=0 Radius=2.75
  constraints (2):
    c: Coincident(g0,g-1)
    c: Radius(g0) = 2.75
FEATURE [PartDesign::Pad] Pad400  label="M3x20 Head034"
  Length = 3
  Length2 = 100
  Profile = -> Sketch948
  Type = 0
FEATURE [Sketcher::SketchObject] Sketch937
  MapMode = 5
  Placement = pos=(0,0,3) rot=(0,0,1;0rad)
  Support = -> [Pad400]
  sketch-geometry (1):
    g0: Circle CenterX=0 CenterY=0 CenterZ=0 NormalX=0 NormalY=0 NormalZ=1 AngleXU=0 Radius=1.5
  constraints (2):
    c: Coincident(g0,g-1)
    c: Radius(g0) = 1.5
FEATURE [PartDesign::Pad] Pad398  label="M3x20 Thread032"
  BaseFeature = -> Pad400
  Length = 20
  Length2 = 100
  Profile = -> Sketch937
  Type = 0
FEATURE [Sketcher::SketchObject] Sketch925
  MapMode = 5
  Placement = pos=(0,0,0) rot=(1,0,0;3.14159rad)
  Support = -> [Pad398]
  sketch-geometry (7):
    g0: LineSegment StartX=1.275 StartY=0.736122 StartZ=0 EndX=0 EndY=1.47224 EndZ=0
    g1: LineSegment StartX=0 StartY=1.47224 StartZ=0 EndX=-1.275 EndY=0.736122 EndZ=0
    g2: LineSegment StartX=-1.275 StartY=0.736122 StartZ=0 EndX=-1.275 EndY=-0.736122 EndZ=0
    g3: LineSegment StartX=-1.275 StartY=-0.736122 StartZ=0 EndX=1.34766e-11 EndY=-1.47224 EndZ=0
    g4: LineSegment StartX=1.34766e-11 StartY=-1.47224 StartZ=0 EndX=1.275 EndY=-0.736122 EndZ=0
    g5: LineSegment StartX=1.275 StartY=-0.736122 StartZ=0 EndX=1.275 EndY=0.736122 EndZ=0
    g6: Circle [constr] CenterX=0 CenterY=0 CenterZ=0 NormalX=0 NormalY=0 NormalZ=1 AngleXU=0 Radius=1.47224
  constraints (16):
    c: Coincident(g0,g1)
    c: Coincident(g1,g2)
    c: Coincident(g2,g3)
    c: Coincident(g3,g4)
    c: Coincident(g4,g5)
    c: Coincident(g5,g0)
    c: Equal(g0, g1-g5) x5
    c: PointOnObject(g0,g6)
    c: PointOnObject(g1,g6)
    c: PointOnObject(g2,g6)
    c: PointOnObject(g3,g6)
    c: PointOnObject(g4,g6)
    c: PointOnObject(g5,g6)
    c: Coincident(g6,g-1)
    c: PointOnObject(g0,g-2)
    c: DistanceX(g1,g0) = 2.55
FEATURE [PartDesign::Pocket] Pocket373  label="M3x20 Wrench029"
  BaseFeature = -> Pad398
  Length = 1.3
  Length2 = 100
  Profile = -> Sketch925
  Type = 0
FEATURE [PartDesign::Chamfer] Chamfer136  label="M3x20 Smooth024"
  Base = -> Pocket373 [Face11,Edge2,Edge24,Edge3]
  BaseFeature = -> Pocket373
  Size = 0.2
FEATURE [PartDesign::Body] Body193  label="M3x041"
  Group = -> [Sketch948,Pad400,Sketch937,Pad398,Sketch925,Pocket373,Chamfer136]
  Origin = -> Origin326
  Placement = pos=(-110.55,-29.35,52.05) rot=(-1,0,0;1.5708rad)
  Tip = -> Chamfer136
FEATURE [Sketcher::SketchObject] Sketch949
  MapMode = 5
  Placement = pos=(0,0,3) rot=(0,0,1;0rad)
  Support = -> [Pad391]
  sketch-geometry (1):
    g0: Circle CenterX=0 CenterY=0 CenterZ=0 NormalX=0 NormalY=0 NormalZ=1 AngleXU=0 Radius=1.5
  constraints (2):
    c: Coincident(g0,g-1)
    c: Radius(g0) = 1.5
FEATURE [PartDesign::Pad] Pad397  label="M3x20 Thread031"
  BaseFeature = -> Pad391
  Length = 20
  Length2 = 100
  Profile = -> Sketch949
  Type = 0
FEATURE [Sketcher::SketchObject] Sketch947
  MapMode = 5
  Placement = pos=(0,0,0) rot=(1,0,0;3.14159rad)
  Support = -> [Pad397]
  sketch-geometry (7):
    g0: LineSegment StartX=1.275 StartY=0.736122 StartZ=0 EndX=0 EndY=1.47224 EndZ=0
    g1: LineSegment StartX=0 StartY=1.47224 StartZ=0 EndX=-1.275 EndY=0.736122 EndZ=0
    g2: LineSegment StartX=-1.275 StartY=0.736122 StartZ=0 EndX=-1.275 EndY=-0.736122 EndZ=0
    g3: LineSegment StartX=-1.275 StartY=-0.736122 StartZ=0 EndX=1.34766e-11 EndY=-1.47224 EndZ=0
    g4: LineSegment StartX=1.34766e-11 StartY=-1.47224 StartZ=0 EndX=1.275 EndY=-0.736122 EndZ=0
    g5: LineSegment StartX=1.275 StartY=-0.736122 StartZ=0 EndX=1.275 EndY=0.736122 EndZ=0
    g6: Circle [constr] CenterX=0 CenterY=0 CenterZ=0 NormalX=0 NormalY=0 NormalZ=1 AngleXU=0 Radius=1.47224
  constraints (16):
    c: Coincident(g0,g1)
    c: Coincident(g1,g2)
    c: Coincident(g2,g3)
    c: Coincident(g3,g4)
    c: Coincident(g4,g5)
    c: Coincident(g5,g0)
    c: Equal(g0, g1-g5) x5
    c: PointOnObject(g0,g6)
    c: PointOnObject(g1,g6)
    c: PointOnObject(g2,g6)
    c: PointOnObject(g3,g6)
    c: PointOnObject(g4,g6)
    c: PointOnObject(g5,g6)
    c: Coincident(g6,g-1)
    c: PointOnObject(g0,g-2)
    c: DistanceX(g1,g0) = 2.55
FEATURE [PartDesign::Pocket] Pocket380  label="M3x20 Wrench034"
  BaseFeature = -> Pad397
  Length = 1.3
  Length2 = 100
  Profile = -> Sketch947
  Type = 0
FEATURE [PartDesign::Chamfer] Chamfer142  label="M3x20 Smooth025"
  Base = -> Pocket380 [Face11,Edge2,Edge24,Edge3]
  BaseFeature = -> Pocket380
  Size = 0.2
FEATURE [PartDesign::Body] Body202  label="M3x046"
  Group = -> [Sketch943,Pad391,Sketch949,Pad397,Sketch947,Pocket380,Chamfer142]
  Origin = -> Origin354
  Placement = pos=(-71.5,-25.55,62.05) rot=(-1,0,0;1.5708rad)
  Tip = -> Chamfer142
FEATURE [Sketcher::SketchObject] Sketch951
  MapMode = 5
  Support = -> [XY_Plane338]
  sketch-geometry (1):
    g0: Circle CenterX=0 CenterY=0 CenterZ=0 NormalX=0 NormalY=0 NormalZ=1 AngleXU=0 Radius=2.75
  constraints (2):
    c: Coincident(g0,g-1)
    c: Radius(g0) = 2.75
FEATURE [PartDesign::Pad] Pad396  label="M3x20 Head033"
  Length = 3
  Length2 = 100
  Profile = -> Sketch951
  Type = 0
FEATURE [Sketcher::SketchObject] Sketch953
  MapMode = 5
  Support = -> [XY_Plane339]
  sketch-geometry (1):
    g0: Circle CenterX=0 CenterY=0 CenterZ=0 NormalX=0 NormalY=0 NormalZ=1 AngleXU=0 Radius=2.75
  constraints (2):
    c: Coincident(g0,g-1)
    c: Radius(g0) = 2.75
FEATURE [Sketcher::SketchObject] Sketch954
  MapMode = 5
  Placement = pos=(0,0,3) rot=(0,0,1;0rad)
  Support = -> [Pad396]
  sketch-geometry (1):
    g0: Circle CenterX=0 CenterY=0 CenterZ=0 NormalX=0 NormalY=0 NormalZ=1 AngleXU=0 Radius=1.5
  constraints (2):
    c: Coincident(g0,g-1)
    c: Radius(g0) = 1.5
FEATURE [Sketcher::SketchObject] Sketch955
  MapMode = 5
  Placement = pos=(0,0,0) rot=(1,0,0;3.14159rad)
  Support = -> [Pad392]
  sketch-geometry (7):
    g0: LineSegment StartX=1.275 StartY=0.736122 StartZ=0 EndX=0 EndY=1.47224 EndZ=0
    g1: LineSegment StartX=0 StartY=1.47224 StartZ=0 EndX=-1.275 EndY=0.736122 EndZ=0
    g2: LineSegment StartX=-1.275 StartY=0.736122 StartZ=0 EndX=-1.275 EndY=-0.736122 EndZ=0
    g3: LineSegment StartX=-1.275 StartY=-0.736122 StartZ=0 EndX=1.34766e-11 EndY=-1.47224 EndZ=0
    g4: LineSegment StartX=1.34766e-11 StartY=-1.47224 StartZ=0 EndX=1.275 EndY=-0.736122 EndZ=0
    g5: LineSegment StartX=1.275 StartY=-0.736122 StartZ=0 EndX=1.275 EndY=0.736122 EndZ=0
    g6: Circle [constr] CenterX=0 CenterY=0 CenterZ=0 NormalX=0 NormalY=0 NormalZ=1 AngleXU=0 Radius=1.47224
  constraints (16):
    c: Coincident(g0,g1)
    c: Coincident(g1,g2)
    c: Coincident(g2,g3)
    c: Coincident(g3,g4)
    c: Coincident(g4,g5)
    c: Coincident(g5,g0)
    c: Equal(g0, g1-g5) x5
    c: PointOnObject(g0,g6)
    c: PointOnObject(g1,g6)
    c: PointOnObject(g2,g6)
    c: PointOnObject(g3,g6)
    c: PointOnObject(g4,g6)
    c: PointOnObject(g5,g6)
    c: Coincident(g6,g-1)
    c: PointOnObject(g0,g-2)
    c: DistanceX(g1,g0) = 2.55
FEATURE [PartDesign::Pocket] Pocket379  label="M3x20 Wrench033"
  BaseFeature = -> Pad392
  Length = 1.3
  Length2 = 100
  Profile = -> Sketch955
  Type = 0
FEATURE [PartDesign::Chamfer] Chamfer212  label="M3x20 Smooth039"
  Base = -> Pocket379 [Face11,Edge2,Edge24,Edge3]
  BaseFeature = -> Pocket379
  Size = 0.2
FEATURE [PartDesign::Body] Body219  label="M3x051"
  Group = -> [Sketch939,Pad389,Sketch940,Pad392,Sketch955,Pocket379,Chamfer212]
  Origin = -> Origin320
  Placement = pos=(-110.55,28,52.05) rot=(1,0,0;1.5708rad)
  Tip = -> Chamfer212
FEATURE [Sketcher::SketchObject] Sketch961
  MapMode = 5
  Support = -> [XY_Plane314]
  sketch-geometry (2):
    g0: Circle CenterX=0 CenterY=0 CenterZ=0 NormalX=0 NormalY=0 NormalZ=1 AngleXU=0 Radius=2.5
    g1: Circle CenterX=0 CenterY=0 CenterZ=0 NormalX=0 NormalY=0 NormalZ=1 AngleXU=0 Radius=1
  constraints (4):
    c: Coincident(g0,g-1)
    c: Coincident(g1,g0)
    c: Radius(g0) = 2.5
    c: Radius(g1) = 1
FEATURE [Sketcher::SketchObject] Sketch963
  MapMode = 5
  Support = -> [XY_Plane345]
  sketch-geometry (13):
    g0: Circle [constr] CenterX=0 CenterY=0 CenterZ=0 NormalX=0 NormalY=0 NormalZ=1 AngleXU=0 Radius=20
    g1: LineSegment [constr] StartX=-14.1421 StartY=14.1421 StartZ=0 EndX=14.1421 EndY=14.1421 EndZ=0
    g2: LineSegment [constr] StartX=14.1421 StartY=14.1421 StartZ=0 EndX=14.1421 EndY=-14.1421 EndZ=0
    g3: LineSegment [constr] StartX=14.1421 StartY=-14.1421 StartZ=0 EndX=-14.1421 EndY=-14.1421 EndZ=0
    g4: LineSegment [constr] StartX=-14.1421 StartY=-14.1421 StartZ=0 EndX=-14.1421 EndY=14.1421 EndZ=0
    g5: ArcOfCircle CenterX=0 CenterY=0 CenterZ=0 NormalX=0 NormalY=0 NormalZ=1 AngleXU=0 Radius=20 StartAngle=2.60685 EndAngle=3.67634
    g6: ArcOfCircle CenterX=-14.1421 CenterY=14.1421 CenterZ=0 NormalX=0 NormalY=0 NormalZ=1 AngleXU=0 Radius=5 StartAngle=0.66007 EndAngle=4.05232
    g7: ArcOfCircle CenterX=14.1421 CenterY=14.1421 CenterZ=0 NormalX=0 NormalY=0 NormalZ=1 AngleXU=0 Radius=5 StartAngle=5.37246 EndAngle=8.76471
    g8: ArcOfCircle CenterX=14.1421 CenterY=-14.1421 CenterZ=0 NormalX=0 NormalY=0 NormalZ=1 AngleXU=0 Radius=5 StartAngle=3.80166 EndAngle=7.19391
    g9: ArcOfCircle CenterX=-14.1421 CenterY=-14.1421 CenterZ=0 NormalX=0 NormalY=0 NormalZ=1 AngleXU=0 Radius=5 StartAngle=2.23087 EndAngle=5.62311
    g10: ArcOfCircle CenterX=0 CenterY=0 CenterZ=0 NormalX=0 NormalY=0 NormalZ=1 AngleXU=0 Radius=20 StartAngle=1.03605 EndAngle=2.10554
    g11: ArcOfCircle CenterX=0 CenterY=0 CenterZ=0 NormalX=0 NormalY=0 NormalZ=1 AngleXU=0 Radius=20 StartAngle=5.74844 EndAngle=6.81793
    g12: ArcOfCircle CenterX=0 CenterY=0 CenterZ=0 NormalX=0 NormalY=0 NormalZ=1 AngleXU=0 Radius=20 StartAngle=4.17765 EndAngle=5.24713
  constraints (38):
    c: Coincident(g0,g-1)
    c: Radius(g0) = 20
    c: Coincident(g1,g2)
    c: Coincident(g2,g3)
    c: Coincident(g3,g4)
    c: Coincident(g4,g1)
    c: Horizontal(g1)
    c: Horizontal(g3)
    c: Vertical(g2)
    c: Vertical(g4)
    c: PointOnObject(g1,g0)
    c: PointOnObject(g2,g0)
    c: Equal(g1,g2)
    c: PointOnObject(g1,g0)
    c: Coincident(g5,g-1)
    c: Radius(g5) = 20
    c: Coincident(g6,g1)
    c: Coincident(g7,g1)
    c: Coincident(g8,g2)
    c: Coincident(g9,g3)
    c: Coincident(g5,g6)
    c: Equal(g5,g10)
    c: Coincident(g10,g7)
    c: Coincident(g5,g10)
    c: Coincident(g11,g7)
    c: Equal(g5,g11)
    c: Coincident(g11,g8)
    c: Coincident(g5,g11)
    c: Coincident(g12,g8)
    c: Equal(g5,g12)
    c: Coincident(g12,g9)
    c: Coincident(g5,g12)
    c: Coincident(g5,g9)
    c: Coincident(g6,g10)
    c: Radius(g6) = 5
    c: Equal(g6,g7)
    c: Equal(g6,g8)
    c: Equal(g6,g9)
FEATURE [Sketcher::SketchObject] Sketch964
  MapMode = 5
  Support = -> [XY_Plane309]
  sketch-geometry (8):
    g0: LineSegment StartX=0 StartY=2.3094 StartZ=0 EndX=-2 EndY=1.1547 EndZ=0
    g1: LineSegment StartX=-2 StartY=1.1547 StartZ=0 EndX=-2 EndY=-1.1547 EndZ=0
    g2: LineSegment StartX=-2 StartY=-1.1547 StartZ=0 EndX=-2e-16 EndY=-2.3094 EndZ=0
    g3: LineSegment StartX=-2e-16 StartY=-2.3094 StartZ=0 EndX=2 EndY=-1.1547 EndZ=0
    g4: LineSegment StartX=2 StartY=-1.1547 StartZ=0 EndX=2 EndY=1.1547 EndZ=0
    g5: LineSegment StartX=2 StartY=1.1547 StartZ=0 EndX=0 EndY=2.3094 EndZ=0
    g6: Circle [constr] CenterX=0 CenterY=0 CenterZ=0 NormalX=0 NormalY=0 NormalZ=1 AngleXU=0 Radius=2.3094
    g7: Circle CenterX=0 CenterY=0 CenterZ=0 NormalX=0 NormalY=0 NormalZ=1 AngleXU=0 Radius=1
  constraints (18):
    c: Coincident(g0,g1)
    c: Coincident(g1,g2)
    c: Coincident(g2,g3)
    c: Coincident(g3,g4)
    c: Coincident(g4,g5)
    c: Coincident(g5,g0)
    c: Equal(g0, g1-g5) x5
    c: PointOnObject(g0,g6)
    c: PointOnObject(g1,g6)
    c: PointOnObject(g2,g6)
    c: PointOnObject(g3,g6)
    c: PointOnObject(g4,g6)
    c: PointOnObject(g5,g6)
    c: Coincident(g6,g-1)
    c: PointOnObject(g5,g-2)
    c: DistanceX(g0,g4) = 4
    c: Coincident(g7,g-1)
    c: Radius(g7) = 1
FEATURE [Sketcher::SketchObject] Sketch965
  MapMode = 5
  Support = -> [XY_Plane378]
FEATURE [Sketcher::SketchObject] Sketch967
  MapMode = 5
  Support = -> [XY_Plane378]
FEATURE [Sketcher::SketchObject] Sketch971
  MapMode = 5
  Support = -> [XY_Plane349]
FEATURE [Sketcher::SketchObject] Sketch975
  MapMode = 5
  Support = -> [XY_Plane375]
  sketch-geometry (8):
    g0: LineSegment StartX=-16.75 StartY=28.25 StartZ=0 EndX=16.75 EndY=28.25 EndZ=0
    g1: LineSegment StartX=21.75 StartY=23.25 StartZ=0 EndX=21.75 EndY=-23.25 EndZ=0
    g2: LineSegment StartX=16.75 StartY=-28.25 StartZ=0 EndX=-16.75 EndY=-28.25 EndZ=0
    g3: LineSegment StartX=-21.75 StartY=-23.25 StartZ=0 EndX=-21.75 EndY=23.25 EndZ=0
    g4: ArcOfCircle CenterX=-16.75 CenterY=23.25 CenterZ=0 NormalX=0 NormalY=0 NormalZ=1 AngleXU=0 Radius=5 StartAngle=1.5708 EndAngle=3.14159
    g5: ArcOfCircle CenterX=16.75 CenterY=23.25 CenterZ=0 NormalX=0 NormalY=0 NormalZ=1 AngleXU=0 Radius=5 StartAngle=1e-16 EndAngle=1.5708
    g6: ArcOfCircle CenterX=16.75 CenterY=-23.25 CenterZ=0 NormalX=0 NormalY=0 NormalZ=1 AngleXU=0 Radius=5 StartAngle=4.71239 EndAngle=6.28319
    g7: ArcOfCircle CenterX=-16.75 CenterY=-23.25 CenterZ=0 NormalX=0 NormalY=0 NormalZ=1 AngleXU=0 Radius=5 StartAngle=3.14159 EndAngle=4.71239
  constraints (18):
    c: Horizontal(g2)
    c: Vertical(g1)
    c: Tangent(g3,g4) = 1.5708
    c: Tangent(g0,g4) = 1.5708
    c: Tangent(g0,g5) = 1.5708
    c: Tangent(g1,g5) = 1.5708
    c: Tangent(g1,g6) = 1.5708
    c: Tangent(g2,g6) = 1.5708
    c: Tangent(g2,g7) = 1.5708
    c: Tangent(g3,g7) = 1.5708
    c: Equal(g4,g5)
    c: Equal(g5,g7)
    c: Equal(g7,g6)
    c: Radius(g5) = 5
    c: DistanceY(g2,g0) = 56.5
    c: DistanceX(g3,g1) = 43.5
    c: Symmetric(g0,g0,g-2)
    c: Symmetric(g3,g3,g-1)
FEATURE [Sketcher::SketchObject] Sketch979
  MapMode = 5
  Support = -> [XY_Plane343]
FEATURE [Sketcher::SketchObject] Sketch983
  MapMode = 5
  Support = -> [XY_Plane333]
  sketch-geometry (64):
    g0: LineSegment [constr] StartX=-3.75 StartY=6.49519 StartZ=0 EndX=-7.5 EndY=0 EndZ=0
    g1: LineSegment [constr] StartX=-7.5 StartY=0 StartZ=0 EndX=-3.75 EndY=-6.49519 EndZ=0
    g2: LineSegment [constr] StartX=-3.75 StartY=-6.49519 StartZ=0 EndX=3.75 EndY=-6.49519 EndZ=0
    g3: LineSegment [constr] StartX=3.75 StartY=-6.49519 StartZ=0 EndX=7.5 EndY=0 EndZ=0
    g4: LineSegment [constr] StartX=7.5 StartY=0 StartZ=0 EndX=3.75 EndY=6.49519 EndZ=0
    g5: LineSegment [constr] StartX=3.75 StartY=6.49519 StartZ=0 EndX=-3.75 EndY=6.49519 EndZ=0
    g6: Circle [constr] CenterX=0 CenterY=0 CenterZ=0 NormalX=0 NormalY=0 NormalZ=1 AngleXU=0 Radius=7.5
    g7: LineSegment [constr] StartX=0 StartY=7.5 StartZ=0 EndX=-6.49519 EndY=3.75 EndZ=0
    g8: LineSegment [constr] StartX=-6.49519 StartY=3.75 StartZ=0 EndX=-6.49519 EndY=-3.75 EndZ=0
    g9: LineSegment [constr] StartX=-6.49519 StartY=-3.75 StartZ=0 EndX=9.8e-15 EndY=-7.5 EndZ=0
    g10: LineSegment [constr] StartX=9.8e-15 StartY=-7.5 StartZ=0 EndX=6.49519 EndY=-3.75 EndZ=0
    g11: LineSegment [constr] StartX=6.49519 StartY=-3.75 StartZ=0 EndX=6.49519 EndY=3.75 EndZ=0
    g12: LineSegment [constr] StartX=6.49519 StartY=3.75 StartZ=0 EndX=0 EndY=7.5 EndZ=0
    g13: Circle [constr] CenterX=0 CenterY=0 CenterZ=0 NormalX=0 NormalY=0 NormalZ=1 AngleXU=0 Radius=7.5
    g14: LineSegment [constr] StartX=0 StartY=10.5 StartZ=0 EndX=-9.09327 EndY=5.25 EndZ=0
    g15: LineSegment [constr] StartX=-9.09327 StartY=5.25 StartZ=0 EndX=-9.09327 EndY=-5.25 EndZ=0
    g16: LineSegment [constr] StartX=-9.09327 StartY=-5.25 StartZ=0 EndX=-1.42e-14 EndY=-10.5 EndZ=0
    g17: LineSegment [constr] StartX=-1.42e-14 StartY=-10.5 StartZ=0 EndX=9.09327 EndY=-5.25 EndZ=0
    g18: LineSegment [constr] StartX=9.09327 StartY=-5.25 StartZ=0 EndX=9.09327 EndY=5.25 EndZ=0
    g19: LineSegment [constr] StartX=9.09327 StartY=5.25 StartZ=0 EndX=0 EndY=10.5 EndZ=0
    g20: Circle [constr] CenterX=0 CenterY=0 CenterZ=0 NormalX=0 NormalY=0 NormalZ=1 AngleXU=0 Radius=10.5
    g21: LineSegment [constr] StartX=0 StartY=13.5 StartZ=0 EndX=-11.6913 EndY=6.75 EndZ=0
    g22: LineSegment [constr] StartX=-11.6913 StartY=6.75 StartZ=0 EndX=-11.6913 EndY=-6.75 EndZ=0
    g23: LineSegment [constr] StartX=-11.6913 StartY=-6.75 StartZ=0 EndX=0 EndY=-13.5 EndZ=0
    g24: LineSegment [constr] StartX=0 StartY=-13.5 StartZ=0 EndX=11.6913 EndY=-6.75 EndZ=0
    g25: LineSegment [constr] StartX=11.6913 StartY=-6.75 StartZ=0 EndX=11.6913 EndY=6.75 EndZ=0
    g26: LineSegment [constr] StartX=11.6913 StartY=6.75 StartZ=0 EndX=0 EndY=13.5 EndZ=0
    g27: Circle [constr] CenterX=0 CenterY=0 CenterZ=0 NormalX=0 NormalY=0 NormalZ=1 AngleXU=0 Radius=13.5
    g28: ArcOfCircle CenterX=0 CenterY=13.5 CenterZ=0 NormalX=0 NormalY=0 NormalZ=1 AngleXU=0 Radius=2.5 StartAngle=0.171439 EndAngle=2.97015
    g29: ArcOfCircle CenterX=11.6913 CenterY=6.75 CenterZ=0 NormalX=0 NormalY=0 NormalZ=1 AngleXU=0 Radius=2.5 StartAngle=5.40743 EndAngle=8.20614
    g30: ArcOfCircle CenterX=11.6913 CenterY=-6.75 CenterZ=0 NormalX=0 NormalY=0 NormalZ=1 AngleXU=0 Radius=2.5 StartAngle=4.36023 EndAngle=7.15894
    g31: ArcOfCircle CenterX=0 CenterY=-13.5 CenterZ=0 NormalX=0 NormalY=0 NormalZ=1 AngleXU=0 Radius=2.5 StartAngle=3.31303 EndAngle=6.11175
    g32: ArcOfCircle CenterX=-11.6913 CenterY=-6.75 CenterZ=0 NormalX=0 NormalY=0 NormalZ=1 AngleXU=0 Radius=2.5 StartAngle=2.26583 EndAngle=5.06455
    g33: ArcOfCircle CenterX=-11.6913 CenterY=6.75 CenterZ=0 NormalX=0 NormalY=0 NormalZ=1 AngleXU=0 Radius=2.5 StartAngle=1.21864 EndAngle=4.01735
    g34: LineSegment StartX=-10.829 StartY=9.09658 StartZ=0 EndX=-3.75 EndY=6.49519 EndZ=0
    g35: LineSegment StartX=-3.75 StartY=6.49519 StartZ=0 EndX=-2.46335 EndY=13.9265 EndZ=0
    g36: LineSegment StartX=2.46335 StartY=13.9265 StartZ=0 EndX=3.75 EndY=6.49519 EndZ=0
    g37: LineSegment StartX=3.75 StartY=6.49519 StartZ=0 EndX=10.829 EndY=9.09658 EndZ=0
    g38: LineSegment StartX=13.2924 StartY=4.82993 StartZ=0 EndX=7.5 EndY=0 EndZ=0
    g39: LineSegment StartX=7.5 StartY=0 StartZ=0 EndX=13.2924 EndY=-4.82993 EndZ=0
    g40: LineSegment StartX=10.829 StartY=-9.09658 StartZ=0 EndX=3.75 EndY=-6.49519 EndZ=0
    g41: LineSegment StartX=3.75 StartY=-6.49519 StartZ=0 EndX=2.46335 EndY=-13.9265 EndZ=0
    g42: LineSegment StartX=-2.46335 StartY=-13.9265 StartZ=0 EndX=-3.75 EndY=-6.49519 EndZ=0
    g43: LineSegment StartX=-3.75 StartY=-6.49519 StartZ=0 EndX=-10.829 EndY=-9.09658 EndZ=0
    g44: LineSegment StartX=-13.2924 StartY=-4.82993 StartZ=0 EndX=-7.5 EndY=0 EndZ=0
    g45: LineSegment StartX=-7.5 StartY=0 StartZ=0 EndX=-13.2924 EndY=4.82993 EndZ=0
    g46: Circle CenterX=-11.6913 CenterY=6.75 CenterZ=0 NormalX=0 NormalY=0 NormalZ=1 AngleXU=0 Radius=0.75
    g47: Circle CenterX=-9.09327 CenterY=5.25 CenterZ=0 NormalX=0 NormalY=0 NormalZ=1 AngleXU=0 Radius=0.75
    g48: Circle CenterX=-6.49519 CenterY=3.75 CenterZ=0 NormalX=0 NormalY=0 NormalZ=1 AngleXU=0 Radius=0.75
    g49: Circle CenterX=0 CenterY=13.5 CenterZ=0 NormalX=0 NormalY=0 NormalZ=1 AngleXU=0 Radius=0.75
    g50: Circle CenterX=0 CenterY=10.5 CenterZ=0 NormalX=0 NormalY=0 NormalZ=1 AngleXU=0 Radius=0.75
    g51: Circle CenterX=0 CenterY=7.5 CenterZ=0 NormalX=0 NormalY=0 NormalZ=1 AngleXU=0 Radius=0.75
    g52: Circle CenterX=11.6913 CenterY=6.75 CenterZ=0 NormalX=0 NormalY=0 NormalZ=1 AngleXU=0 Radius=0.75
    g53: Circle CenterX=9.09327 CenterY=5.25 CenterZ=0 NormalX=0 NormalY=0 NormalZ=1 AngleXU=0 Radius=0.75
    g54: Circle CenterX=6.49519 CenterY=3.75 CenterZ=0 NormalX=0 NormalY=0 NormalZ=1 AngleXU=0 Radius=0.75
    g55: Circle CenterX=11.6913 CenterY=-6.75 CenterZ=0 NormalX=0 NormalY=0 NormalZ=1 AngleXU=0 Radius=0.75
    g56: Circle CenterX=9.09327 CenterY=-5.25 CenterZ=0 NormalX=0 NormalY=0 NormalZ=1 AngleXU=0 Radius=0.75
    g57: Circle CenterX=6.49519 CenterY=-3.75 CenterZ=0 NormalX=0 NormalY=0 NormalZ=1 AngleXU=0 Radius=0.75
    g58: Circle CenterX=9.8e-15 CenterY=-7.5 CenterZ=0 NormalX=0 NormalY=0 NormalZ=1 AngleXU=0 Radius=0.75
    g59: Circle CenterX=-1.42e-14 CenterY=-10.5 CenterZ=0 NormalX=0 NormalY=0 NormalZ=1 AngleXU=0 Radius=0.75
    g60: Circle CenterX=0 CenterY=-13.5 CenterZ=0 NormalX=0 NormalY=0 NormalZ=1 AngleXU=0 Radius=0.75
    g61: Circle CenterX=-11.6913 CenterY=-6.75 CenterZ=0 NormalX=0 NormalY=0 NormalZ=1 AngleXU=0 Radius=0.75
    g62: Circle CenterX=-9.09327 CenterY=-5.25 CenterZ=0 NormalX=0 NormalY=0 NormalZ=1 AngleXU=0 Radius=0.75
    g63: Circle CenterX=-6.49519 CenterY=-3.75 CenterZ=0 NormalX=0 NormalY=0 NormalZ=1 AngleXU=0 Radius=0.75
  constraints (136):
    c: Coincident(g0,g1)
    c: Coincident(g1,g2)
    c: Coincident(g2,g3)
    c: Coincident(g3,g4)
    c: Coincident(g4,g5)
    c: Coincident(g5,g0)
    c: Equal(g0, g1-g5) x5
    c: PointOnObject(g0,g6)
    c: PointOnObject(g1,g6)
    c: PointOnObject(g2,g6)
    c: PointOnObject(g3,g6)
    c: PointOnObject(g4,g6)
    c: PointOnObject(g5,g6)
    c: Coincident(g6,g-1)
    c: Coincident(g7,g8)
    c: Coincident(g8,g9)
    c: Coincident(g9,g10)
    c: Coincident(g10,g11)
    c: Coincident(g11,g12)
    c: Coincident(g12,g7)
    c: Equal(g7, g8-g12) x5
    c: PointOnObject(g7,g13)
    c: PointOnObject(g8,g13)
    c: PointOnObject(g9,g13)
    c: PointOnObject(g10,g13)
    c: PointOnObject(g11,g13)
    c: PointOnObject(g12,g13)
    c: Coincident(g13,g-1)
    c: PointOnObject(g12,g6)
    c: PointOnObject(g7,g-2)
    c: Horizontal(g5)
    c: Radius(g6) = 7.5
    c: Coincident(g14,g15)
    c: Coincident(g15,g16)
    c: Coincident(g16,g17)
    c: Coincident(g17,g18)
    c: Coincident(g18,g19)
    c: Coincident(g19,g14)
    c: Equal(g14, g15-g19) x5
    c: PointOnObject(g14,g20)
    c: PointOnObject(g15,g20)
    c: PointOnObject(g16,g20)
    c: PointOnObject(g17,g20)
    c: PointOnObject(g18,g20)
    c: PointOnObject(g19,g20)
    c: Coincident(g20,g-1)
    c: PointOnObject(g19,g-2)
    c: Radius(g20) = 10.5
    c: Coincident(g21,g22)
    c: Coincident(g22,g23)
    c: Coincident(g23,g24)
    c: Coincident(g24,g25)
    c: Coincident(g25,g26)
    c: Coincident(g26,g21)
    c: Equal(g21, g22-g26) x5
    c: PointOnObject(g21,g27)
    c: PointOnObject(g22,g27)
    c: PointOnObject(g23,g27)
    c: PointOnObject(g24,g27)
    c: PointOnObject(g25,g27)
    c: PointOnObject(g26,g27)
    c: Coincident(g27,g-1)
    c: PointOnObject(g26,g-2)
    c: Radius(g27) = 13.5
    c: Coincident(g28,g21)
    c: Coincident(g29,g25)
    c: Coincident(g30,g24)
    c: Coincident(g31,g23)
    c: Coincident(g32,g22)
    c: Coincident(g33,g21)
    c: Coincident(g34,g0)
    c: Coincident(g35,g34)
    c: Coincident(g36,g4)
    c: Coincident(g37,g36)
    c: Coincident(g38,g3)
    c: Coincident(g39,g38)
    c: Coincident(g40,g2)
    c: Coincident(g41,g40)
    c: Coincident(g42,g1)
    c: Coincident(g43,g42)
    c: Coincident(g44,g0)
    c: Coincident(g45,g44)
    c: Tangent(g35,g28) = 1.5708
    c: Tangent(g36,g28) = 1.5708
    c: Tangent(g37,g29) = 1.5708
    c: Tangent(g38,g29) = 1.5708
    c: Tangent(g39,g30) = 1.5708
    c: Tangent(g40,g30) = 1.5708
    c: Tangent(g41,g31) = 1.5708
    c: Tangent(g42,g31) = 1.5708
    c: Tangent(g43,g32) = 1.5708
    c: Tangent(g44,g32) = 1.5708
    c: Tangent(g45,g33) = 1.5708
    c: Tangent(g34,g33) = 1.5708
    c: Radius(g29) = 2.5
    c: Equal(g29,g28)
    c: Equal(g28,g33)
    c: Equal(g33,g32)
    c: Equal(g32,g31)
    c: Equal(g31,g30)
    c: Coincident(g46,g33)
    c: Coincident(g47,g14)
    c: Coincident(g48,g7)
    c: Coincident(g49,g28)
    c: Coincident(g50,g14)
    c: Coincident(g51,g7)
    c: Coincident(g52,g29)
    c: Coincident(g53,g18)
    c: Coincident(g54,g11)
    c: Coincident(g55,g30)
    c: Coincident(g56,g17)
    c: Coincident(g57,g10)
    c: Coincident(g58,g9)
    c: Coincident(g59,g16)
    c: Coincident(g60,g31)
    c: Coincident(g61,g32)
    c: Coincident(g62,g15)
    c: Coincident(g63,g8)
    c: Equal(g61,g62)
    c: Equal(g62,g63)
    c: Equal(g63,g58)
    c: Equal(g58,g59)
    c: Equal(g59,g60)
    c: Equal(g60,g55)
    c: Equal(g55,g56)
    c: Equal(g56,g57)
    c: Equal(g57,g54)
    c: Equal(g54,g53)
    c: Equal(g53,g52)
    c: Equal(g52,g51)
    c: Equal(g51,g50)
    c: Equal(g50,g49)
    c: Equal(g49,g46)
    c: Equal(g46,g47)
    c: Equal(g47,g48)
    c: Radius(g55) = 0.75
FEATURE [Sketcher::SketchObject] Sketch984
  MapMode = 5
  Support = -> [XY_Plane343]
FEATURE [Sketcher::SketchObject] Sketch985
  MapMode = 5
  Support = -> [XY_Plane378]
  sketch-geometry (8):
    g0: LineSegment StartX=0 StartY=2.3094 StartZ=0 EndX=-2 EndY=1.1547 EndZ=0
    g1: LineSegment StartX=-2 StartY=1.1547 StartZ=0 EndX=-2 EndY=-1.1547 EndZ=0
    g2: LineSegment StartX=-2 StartY=-1.1547 StartZ=0 EndX=-2e-16 EndY=-2.3094 EndZ=0
    g3: LineSegment StartX=-2e-16 StartY=-2.3094 StartZ=0 EndX=2 EndY=-1.1547 EndZ=0
    g4: LineSegment StartX=2 StartY=-1.1547 StartZ=0 EndX=2 EndY=1.1547 EndZ=0
    g5: LineSegment StartX=2 StartY=1.1547 StartZ=0 EndX=0 EndY=2.3094 EndZ=0
    g6: Circle [constr] CenterX=0 CenterY=0 CenterZ=0 NormalX=0 NormalY=0 NormalZ=1 AngleXU=0 Radius=2.3094
    g7: Circle CenterX=0 CenterY=0 CenterZ=0 NormalX=0 NormalY=0 NormalZ=1 AngleXU=0 Radius=1
  constraints (18):
    c: Coincident(g0,g1)
    c: Coincident(g1,g2)
    c: Coincident(g2,g3)
    c: Coincident(g3,g4)
    c: Coincident(g4,g5)
    c: Coincident(g5,g0)
    c: Equal(g0, g1-g5) x5
    c: PointOnObject(g0,g6)
    c: PointOnObject(g1,g6)
    c: PointOnObject(g2,g6)
    c: PointOnObject(g3,g6)
    c: PointOnObject(g4,g6)
    c: PointOnObject(g5,g6)
    c: Coincident(g6,g-1)
    c: PointOnObject(g5,g-2)
    c: DistanceX(g0,g4) = 4
    c: Coincident(g7,g-1)
    c: Radius(g7) = 1
FEATURE [Sketcher::SketchObject] Sketch986
  MapMode = 5
  Support = -> [XY_Plane373]
  sketch-geometry (1):
    g0: Circle CenterX=0 CenterY=0 CenterZ=0 NormalX=0 NormalY=0 NormalZ=1 AngleXU=0 Radius=1.9
  constraints (2):
    c: Coincident(g0,g-1)
    c: Radius(g0) = 1.9
FEATURE [Sketcher::SketchObject] Sketch988
  MapMode = 5
  Support = -> [XY_Plane315]
  sketch-geometry (1):
    g0: Circle CenterX=0 CenterY=0 CenterZ=0 NormalX=0 NormalY=0 NormalZ=1 AngleXU=0 Radius=1.9
  constraints (2):
    c: Coincident(g0,g-1)
    c: Radius(g0) = 1.9
FEATURE [PartDesign::Pad] Pad402  label="M3x20 Head035"
  Length = 3
  Length2 = 100
  Profile = -> Sketch953
  Type = 0
FEATURE [Sketcher::SketchObject] Sketch942
  MapMode = 5
  Placement = pos=(0,0,3) rot=(0,0,1;0rad)
  Support = -> [Pad402]
  sketch-geometry (1):
    g0: Circle CenterX=0 CenterY=0 CenterZ=0 NormalX=0 NormalY=0 NormalZ=1 AngleXU=0 Radius=1.5
  constraints (2):
    c: Coincident(g0,g-1)
    c: Radius(g0) = 1.5
FEATURE [PartDesign::Pad] Pad394  label="M3x20 Thread030"
  BaseFeature = -> Pad402
  Length = 20
  Length2 = 100
  Profile = -> Sketch942
  Type = 0
FEATURE [Sketcher::SketchObject] Sketch952
  MapMode = 5
  Placement = pos=(0,0,0) rot=(1,0,0;3.14159rad)
  Support = -> [Pad394]
  sketch-geometry (7):
    g0: LineSegment StartX=1.275 StartY=0.736122 StartZ=0 EndX=0 EndY=1.47224 EndZ=0
    g1: LineSegment StartX=0 StartY=1.47224 StartZ=0 EndX=-1.275 EndY=0.736122 EndZ=0
    g2: LineSegment StartX=-1.275 StartY=0.736122 StartZ=0 EndX=-1.275 EndY=-0.736122 EndZ=0
    g3: LineSegment StartX=-1.275 StartY=-0.736122 StartZ=0 EndX=1.34766e-11 EndY=-1.47224 EndZ=0
    g4: LineSegment StartX=1.34766e-11 StartY=-1.47224 StartZ=0 EndX=1.275 EndY=-0.736122 EndZ=0
    g5: LineSegment StartX=1.275 StartY=-0.736122 StartZ=0 EndX=1.275 EndY=0.736122 EndZ=0
    g6: Circle [constr] CenterX=0 CenterY=0 CenterZ=0 NormalX=0 NormalY=0 NormalZ=1 AngleXU=0 Radius=1.47224
  constraints (16):
    c: Coincident(g0,g1)
    c: Coincident(g1,g2)
    c: Coincident(g2,g3)
    c: Coincident(g3,g4)
    c: Coincident(g4,g5)
    c: Coincident(g5,g0)
    c: Equal(g0, g1-g5) x5
    c: PointOnObject(g0,g6)
    c: PointOnObject(g1,g6)
    c: PointOnObject(g2,g6)
    c: PointOnObject(g3,g6)
    c: PointOnObject(g4,g6)
    c: PointOnObject(g5,g6)
    c: Coincident(g6,g-1)
    c: PointOnObject(g0,g-2)
    c: DistanceX(g1,g0) = 2.55
FEATURE [PartDesign::Pocket] Pocket376  label="M3x20 Wrench031"
  BaseFeature = -> Pad394
  Length = 1.3
  Length2 = 100
  Profile = -> Sketch952
  Type = 0
FEATURE [PartDesign::Chamfer] Chamfer206  label="M3x20 Smooth036"
  Base = -> Pocket376 [Face11,Edge2,Edge24,Edge3]
  BaseFeature = -> Pocket376
  Size = 0.2
FEATURE [PartDesign::Body] Body200  label="M3x044"
  Group = -> [Sketch953,Pad402,Sketch942,Pad394,Sketch952,Pocket376,Chamfer206]
  Origin = -> Origin258
  Placement = pos=(-115.35,28,62.05) rot=(1,0,0;1.5708rad)
  Tip = -> Chamfer206
FEATURE [App::Part] Part102  label="Shell Screws001"
  Group = -> [Body218,Body193,Body200,Body219]
  Origin = -> Origin283
FEATURE [PartDesign::Pad] Pad403
  Length = 2
  Length2 = 100
  Profile = -> Sketch983
  Type = 0
FEATURE [Sketcher::SketchObject] Sketch957
  MapMode = 5
  Placement = pos=(0,0,2) rot=(0,0,1;0rad)
  Support = -> [Pad403]
  sketch-geometry (2):
    g0: Circle CenterX=0 CenterY=0 CenterZ=0 NormalX=0 NormalY=0 NormalZ=1 AngleXU=0 Radius=5
    g1: Circle CenterX=0 CenterY=0 CenterZ=0 NormalX=0 NormalY=0 NormalZ=1 AngleXU=0 Radius=3.5
  constraints (4):
    c: Coincident(g0,g-1)
    c: Coincident(g1,g0)
    c: Radius(g1) = 3.5
    c: Radius(g0) = 5
FEATURE [PartDesign::Pocket] Pocket384  label="M3x20 Wrench035"
  BaseFeature = -> Pad401
  Length = 1.3
  Length2 = 100
  Profile = -> Sketch938
  Type = 0
FEATURE [PartDesign::Chamfer] Chamfer207  label="M3x20 Smooth037"
  Base = -> Pocket384 [Face11,Edge2,Edge24,Edge3]
  BaseFeature = -> Pocket384
  Size = 0.2
FEATURE [PartDesign::Body] Body215  label="M3x048"
  Group = -> [Sketch924,Pad387,Sketch941,Pad401,Sketch938,Pocket384,Chamfer207]
  Origin = -> Origin372
  Placement = pos=(-71.6,-25.55,52.05) rot=(-1,0,0;1.5708rad)
  Tip = -> Chamfer207
FEATURE [PartDesign::Pad] Pad404  label="M3x8 Head044"
  Length = 3
  Length2 = 100
  Profile = -> Sketch945
  Type = 0
FEATURE [Sketcher::SketchObject] Sketch950
  MapMode = 5
  Placement = pos=(0,0,3) rot=(0,0,1;0rad)
  Support = -> [Pad404]
  sketch-geometry (1):
    g0: Circle CenterX=0 CenterY=0 CenterZ=0 NormalX=0 NormalY=0 NormalZ=1 AngleXU=0 Radius=1.5
  constraints (2):
    c: Coincident(g0,g-1)
    c: Radius(g0) = 1.5
FEATURE [PartDesign::Pad] Pad395  label="M3x8 Thread044"
  BaseFeature = -> Pad404
  Length = 8
  Length2 = 100
  Profile = -> Sketch950
  Type = 0
FEATURE [Sketcher::SketchObject] Sketch960
  MapMode = 5
  Placement = pos=(0,0,0) rot=(1,0,0;3.14159rad)
  Support = -> [Pad395]
  sketch-geometry (7):
    g0: LineSegment StartX=1.275 StartY=0.736122 StartZ=0 EndX=0 EndY=1.47224 EndZ=0
    g1: LineSegment StartX=0 StartY=1.47224 StartZ=0 EndX=-1.275 EndY=0.736122 EndZ=0
    g2: LineSegment StartX=-1.275 StartY=0.736122 StartZ=0 EndX=-1.275 EndY=-0.736122 EndZ=0
    g3: LineSegment StartX=-1.275 StartY=-0.736122 StartZ=0 EndX=1.34766e-11 EndY=-1.47224 EndZ=0
    g4: LineSegment StartX=1.34766e-11 StartY=-1.47224 StartZ=0 EndX=1.275 EndY=-0.736122 EndZ=0
    g5: LineSegment StartX=1.275 StartY=-0.736122 StartZ=0 EndX=1.275 EndY=0.736122 EndZ=0
    g6: Circle [constr] CenterX=0 CenterY=0 CenterZ=0 NormalX=0 NormalY=0 NormalZ=1 AngleXU=0 Radius=1.47224
  constraints (16):
    c: Coincident(g0,g1)
    c: Coincident(g1,g2)
    c: Coincident(g2,g3)
    c: Coincident(g3,g4)
    c: Coincident(g4,g5)
    c: Coincident(g5,g0)
    c: Equal(g0, g1-g5) x5
    c: PointOnObject(g0,g6)
    c: PointOnObject(g1,g6)
    c: PointOnObject(g2,g6)
    c: PointOnObject(g3,g6)
    c: PointOnObject(g4,g6)
    c: PointOnObject(g5,g6)
    c: Coincident(g6,g-1)
    c: PointOnObject(g0,g-2)
    c: DistanceX(g1,g0) = 2.55
FEATURE [PartDesign::Pocket] Pocket381  label="M3x8 Wrench044"
  BaseFeature = -> Pad395
  Length = 1.3
  Length2 = 100
  Profile = -> Sketch960
  Type = 0
FEATURE [PartDesign::Chamfer] Chamfer150  label="M3x8 Smooth040"
  Base = -> Pocket381 [Face11,Edge2,Edge24,Edge3]
  BaseFeature = -> Pocket381
  Size = 0.2
FEATURE [PartDesign::Body] Body198  label="M3x043"
  Group = -> [Sketch945,Pad404,Sketch950,Pad395,Sketch960,Pocket381,Chamfer150]
  Origin = -> Origin381
  Placement = pos=(-144.1,-31.4,27.05) rot=(-1,0,0;1.5708rad)
  Tip = -> Chamfer150
FEATURE [PartDesign::Pad] Pad406  label="M3x20 Thread035"
  BaseFeature = -> Pad396
  Length = 20
  Length2 = 100
  Profile = -> Sketch954
  Type = 0
FEATURE [Sketcher::SketchObject] Sketch956
  MapMode = 5
  Placement = pos=(0,0,0) rot=(1,0,0;3.14159rad)
  Support = -> [Pad406]
  sketch-geometry (7):
    g0: LineSegment StartX=1.275 StartY=0.736122 StartZ=0 EndX=0 EndY=1.47224 EndZ=0
    g1: LineSegment StartX=0 StartY=1.47224 StartZ=0 EndX=-1.275 EndY=0.736122 EndZ=0
    g2: LineSegment StartX=-1.275 StartY=0.736122 StartZ=0 EndX=-1.275 EndY=-0.736122 EndZ=0
    g3: LineSegment StartX=-1.275 StartY=-0.736122 StartZ=0 EndX=1.34766e-11 EndY=-1.47224 EndZ=0
    g4: LineSegment StartX=1.34766e-11 StartY=-1.47224 StartZ=0 EndX=1.275 EndY=-0.736122 EndZ=0
    g5: LineSegment StartX=1.275 StartY=-0.736122 StartZ=0 EndX=1.275 EndY=0.736122 EndZ=0
    g6: Circle [constr] CenterX=0 CenterY=0 CenterZ=0 NormalX=0 NormalY=0 NormalZ=1 AngleXU=0 Radius=1.47224
  constraints (16):
    c: Coincident(g0,g1)
    c: Coincident(g1,g2)
    c: Coincident(g2,g3)
    c: Coincident(g3,g4)
    c: Coincident(g4,g5)
    c: Coincident(g5,g0)
    c: Equal(g0, g1-g5) x5
    c: PointOnObject(g0,g6)
    c: PointOnObject(g1,g6)
    c: PointOnObject(g2,g6)
    c: PointOnObject(g3,g6)
    c: PointOnObject(g4,g6)
    c: PointOnObject(g5,g6)
    c: Coincident(g6,g-1)
    c: PointOnObject(g0,g-2)
    c: DistanceX(g1,g0) = 2.55
FEATURE [PartDesign::Pocket] Pocket375  label="M3x20 Wrench030"
  BaseFeature = -> Pad406
  Length = 1.3
  Length2 = 100
  Profile = -> Sketch956
  Type = 0
FEATURE [PartDesign::Chamfer] Chamfer211  label="M3x20 Smooth038"
  Base = -> Pocket375 [Face11,Edge2,Edge24,Edge3]
  BaseFeature = -> Pocket375
  Size = 0.2
FEATURE [PartDesign::Body] Body216  label="M3x049"
  Group = -> [Sketch951,Pad396,Sketch954,Pad406,Sketch956,Pocket375,Chamfer211]
  Origin = -> Origin382
  Placement = pos=(-23.1,-25.6,52) rot=(-1,0,0;1.5708rad)
  Tip = -> Chamfer211
FEATURE [App::Part] Part103  label="Servo Screws001"
  Group = -> [Body202,Body215,Body197,Body216]
  Origin = -> Origin380
FEATURE [PartDesign::Pad] Pad407  label="M3x8 Head045"
  Length = 2
  Length2 = 100
  Profile = -> Sketch988
  Type = 0
FEATURE [PartDesign::Pad] Pad409  label="Ball Bearing Pin003"
  Length = 5
  Length2 = 100
  Profile = -> Sketch961
  Type = 0
FEATURE [PartDesign::Chamfer] Chamfer146  label="Smooth Pinhead002"
  Base = -> Pad409 [Edge3]
  BaseFeature = -> Pad409
  Size = 0.4
FEATURE [PartDesign::Body] Body266  label="Shoulder_Joint_Ball_Bearing_Pin003"
  Group = -> [Sketch961,Pad409,Chamfer146]
  Origin = -> Origin273
  Placement = pos=(-21.75,10,15) rot=(0,-1,0;1.5708rad)
  Tip = -> Chamfer146
FEATURE [PartDesign::Pocket] Pocket389
  BaseFeature = -> Pad403
  Length = 1
  Length2 = 100
  Profile = -> Sketch957
  Type = 0
FEATURE [Sketcher::SketchObject] Sketch972
  MapMode = 5
  Placement = pos=(0,0,2) rot=(0,0,1;0rad)
  Support = -> [Pocket389]
  sketch-geometry (1):
    g0: Circle CenterX=0 CenterY=0 CenterZ=0 NormalX=0 NormalY=0 NormalZ=1 AngleXU=0 Radius=3
  constraints (2):
    c: Coincident(g0,g-1)
    c: Radius(g0) = 3
FEATURE [PartDesign::Pocket] Pocket388
  BaseFeature = -> Pocket389
  Length = 1
  Length2 = 100
  Profile = -> Sketch972
  Type = 0
FEATURE [Sketcher::SketchObject] Sketch968
  MapMode = 5
  Placement = pos=(0,0,1) rot=(0,0,1;0rad)
  Support = -> [Pocket388]
  sketch-geometry (1):
    g0: Circle CenterX=0 CenterY=0 CenterZ=0 NormalX=0 NormalY=0 NormalZ=1 AngleXU=0 Radius=1.5
  constraints (2):
    c: Coincident(g0,g-1)
    c: Radius(g0) = 1.5
FEATURE [PartDesign::Pocket] Pocket385
  BaseFeature = -> Pocket388
  Length = 5
  Length2 = 100
  Profile = -> Sketch968
  Type = 0
FEATURE [PartDesign::Pad] Pad413  label="M3x8 Head048"
  Length = 2
  Length2 = 100
  Profile = -> Sketch986
  Type = 0
FEATURE [PartDesign::Pad] Pad428  label="M3 Nut Primitive081"
  Length = 0.6
  Length2 = 0.6
  Profile = -> Sketch964
  Type = 4
FEATURE [PartDesign::Pad] Pad429  label="M3 Nut Primitive082"
  Length = 0.6
  Length2 = 0.6
  Profile = -> Sketch985
  Type = 4
FEATURE [PartDesign::Pad] Pad442  label="Baseplate019"
  Length = 5
  Length2 = 100
  Profile = -> Sketch975
  Type = 0
FEATURE [PartDesign::Pad] Pad435  label="Baseplate Expansion001"
  BaseFeature = -> Pad442
  Length = 20
  Length2 = 100
  Profile = -> Pad442 [Face10]
  Type = 0
FEATURE [Sketcher::SketchObject] Sketch981
  MapMode = 5
  Placement = pos=(0,0,25) rot=(0,0,1;0rad)
  Support = -> [Pad435]
  sketch-geometry (8):
    g0: LineSegment StartX=9.75 StartY=28.25 StartZ=0 EndX=9.75 EndY=20.25 EndZ=0
    g1: LineSegment StartX=9.75 StartY=20.25 StartZ=0 EndX=-18.75 EndY=20.25 EndZ=0
    g2: LineSegment StartX=-18.75 StartY=20.25 StartZ=0 EndX=-18.75 EndY=-20.25 EndZ=0
    g3: LineSegment StartX=-18.75 StartY=-20.25 StartZ=0 EndX=9.75 EndY=-20.25 EndZ=0
    g4: LineSegment StartX=9.75 StartY=-20.25 StartZ=0 EndX=9.75 EndY=-28.25 EndZ=0
    g5: LineSegment StartX=9.75 StartY=-28.25 StartZ=0 EndX=21.75 EndY=-28.25 EndZ=0
    g6: LineSegment StartX=21.75 StartY=-28.25 StartZ=0 EndX=21.75 EndY=28.25 EndZ=0
    g7: LineSegment StartX=21.75 StartY=28.25 StartZ=0 EndX=9.75 EndY=28.25 EndZ=0
  constraints (22):
    c: Vertical(g0)
    c: Coincident(g0,g1)
    c: Horizontal(g1)
    c: Coincident(g1,g2)
    c: Coincident(g2,g3)
    c: Horizontal(g3)
    c: Coincident(g3,g4)
    c: Vertical(g4)
    c: Coincident(g4,g5)
    c: Horizontal(g5)
    c: Coincident(g5,g6)
    c: Coincident(g6,g7)
    c: Coincident(g7,g0)
    c: Horizontal(g7)
    c: Equal(g7,g5)
    c: Symmetric(g6,g5,g-1)
    c: Symmetric(g1,g2,g-1)
    c: DistanceY(g6,g6) = 56.5
    c: DistanceX(g-1,g6) = 21.75
    c: DistanceX(g1,g-1) = 18.75
    c: DistanceY(g0,g0) = 8
    c: DistanceX(g1,g0) = 28.5
FEATURE [PartDesign::Pocket] Pocket397  label="Servo Pocket007"
  BaseFeature = -> Pad435
  Length = 20
  Length2 = 100
  Profile = -> Sketch981
  Type = 0
FEATURE [Sketcher::SketchObject] Sketch974
  MapMode = 5
  Placement = pos=(0,0,5) rot=(0,0,1;0rad)
  Support = -> [Pocket397]
  sketch-geometry (1):
    g0: Circle CenterX=0 CenterY=0 CenterZ=0 NormalX=0 NormalY=0 NormalZ=1 AngleXU=0 Radius=16.5
  constraints (2):
    c: Coincident(g0,g-1)
    c: Radius(g0) = 16.5
FEATURE [PartDesign::Pocket] Pocket398  label="Accesshole Servohorn Cap001"
  BaseFeature = -> Pocket397
  Length = 5
  Length2 = 100
  Profile = -> Sketch974
  Type = 0
FEATURE [Sketcher::SketchObject] Sketch959
  MapMode = 5
  Placement = pos=(0,0,5) rot=(0,0,1;0rad)
  Support = -> [Pocket398]
  sketch-geometry (9):
    g0: Circle [constr] CenterX=0 CenterY=0 CenterZ=0 NormalX=0 NormalY=0 NormalZ=1 AngleXU=0 Radius=20
    g1: LineSegment [constr] StartX=-14.1421 StartY=14.1421 StartZ=0 EndX=14.1421 EndY=14.1421 EndZ=0
    g2: LineSegment [constr] StartX=14.1421 StartY=14.1421 StartZ=0 EndX=14.1421 EndY=-14.1421 EndZ=0
    g3: LineSegment [constr] StartX=14.1421 StartY=-14.1421 StartZ=0 EndX=-14.1421 EndY=-14.1421 EndZ=0
    g4: LineSegment [constr] StartX=-14.1421 StartY=-14.1421 StartZ=0 EndX=-14.1421 EndY=14.1421 EndZ=0
    g5: Circle CenterX=-14.1421 CenterY=14.1421 CenterZ=0 NormalX=0 NormalY=0 NormalZ=1 AngleXU=0 Radius=1.6
    g6: Circle CenterX=14.1421 CenterY=14.1421 CenterZ=0 NormalX=0 NormalY=0 NormalZ=1 AngleXU=0 Radius=1.6
    g7: Circle CenterX=14.1421 CenterY=-14.1421 CenterZ=0 NormalX=0 NormalY=0 NormalZ=1 AngleXU=0 Radius=1.6
    g8: Circle CenterX=-14.1421 CenterY=-14.1421 CenterZ=0 NormalX=0 NormalY=0 NormalZ=1 AngleXU=0 Radius=1.6
  constraints (22):
    c: Coincident(g0,g-1)
    c: Radius(g0) = 20
    c: Coincident(g1,g2)
    c: Coincident(g2,g3)
    c: Coincident(g3,g4)
    c: Coincident(g4,g1)
    c: Horizontal(g1)
    c: Horizontal(g3)
    c: Vertical(g2)
    c: Vertical(g4)
    c: PointOnObject(g1,g0)
    c: PointOnObject(g2,g0)
    c: PointOnObject(g1,g0)
    c: Equal(g1,g2)
    c: Coincident(g5,g1)
    c: Coincident(g6,g1)
    c: Coincident(g7,g2)
    c: Coincident(g8,g3)
    c: Radius(g5) = 1.6
    c: Equal(g5,g6)
    c: Equal(g5,g7)
    c: Equal(g5,g8)
FEATURE [PartDesign::Pocket] Pocket386  label="Screwholes Servohorn Cap001"
  BaseFeature = -> Pocket398
  Length = 5
  Length2 = 100
  Profile = -> Sketch959
  Type = 0
FEATURE [Sketcher::SketchObject] Sketch976
  MapMode = 5
  Placement = pos=(0,0,5) rot=(0,0,1;0rad)
  Support = -> [Pocket386]
  sketch-geometry (35):
    g0: Circle [constr] CenterX=0 CenterY=0 CenterZ=0 NormalX=0 NormalY=0 NormalZ=1 AngleXU=0 Radius=20
    g1: LineSegment [constr] StartX=-14.1421 StartY=14.1421 StartZ=0 EndX=14.1421 EndY=-14.1421 EndZ=0
    g2: LineSegment [constr] StartX=14.1421 StartY=14.1421 StartZ=0 EndX=-14.1421 EndY=-14.1421 EndZ=0
    g3: LineSegment [constr] StartX=-14.1421 StartY=14.1421 StartZ=0 EndX=14.1421 EndY=14.1421 EndZ=0
    g4: LineSegment [constr] StartX=14.1421 StartY=14.1421 StartZ=0 EndX=14.1421 EndY=-14.1421 EndZ=0
    g5: LineSegment [constr] StartX=14.1421 StartY=-14.1421 StartZ=0 EndX=-14.1421 EndY=-14.1421 EndZ=0
    g6: LineSegment [constr] StartX=-14.1421 StartY=-14.1421 StartZ=0 EndX=-14.1421 EndY=14.1421 EndZ=0
    g7: LineSegment StartX=-11.8151 StartY=16.4692 StartZ=0 EndX=-14.9939 EndY=17.3209 EndZ=0
    g8: LineSegment StartX=-14.9939 StartY=17.3209 StartZ=0 EndX=-17.3209 EndY=14.9939 EndZ=0
    g9: LineSegment StartX=-17.3209 StartY=14.9939 StartZ=0 EndX=-16.4692 EndY=11.8151 EndZ=0
    g10: LineSegment StartX=-16.4692 StartY=11.8151 StartZ=0 EndX=-13.2904 EndY=10.9634 EndZ=0
    g11: LineSegment StartX=-13.2904 StartY=10.9634 StartZ=0 EndX=-10.9634 EndY=13.2904 EndZ=0
    g12: LineSegment StartX=-10.9634 StartY=13.2904 StartZ=0 EndX=-11.8151 EndY=16.4692 EndZ=0
    g13: Circle [constr] CenterX=-14.1421 CenterY=14.1421 CenterZ=0 NormalX=0 NormalY=0 NormalZ=1 AngleXU=0 Radius=3.2909
    g14: LineSegment StartX=14.9939 StartY=17.3209 StartZ=0 EndX=11.8151 EndY=16.4692 EndZ=0
    g15: LineSegment StartX=11.8151 StartY=16.4692 StartZ=0 EndX=10.9634 EndY=13.2904 EndZ=0
    g16: LineSegment StartX=10.9634 StartY=13.2904 StartZ=0 EndX=13.2904 EndY=10.9634 EndZ=0
    g17: LineSegment StartX=13.2904 StartY=10.9634 StartZ=0 EndX=16.4692 EndY=11.8151 EndZ=0
    g18: LineSegment StartX=16.4692 StartY=11.8151 StartZ=0 EndX=17.3209 EndY=14.9939 EndZ=0
    g19: LineSegment StartX=17.3209 StartY=14.9939 StartZ=0 EndX=14.9939 EndY=17.3209 EndZ=0
    g20: Circle [constr] CenterX=14.1421 CenterY=14.1421 CenterZ=0 NormalX=0 NormalY=0 NormalZ=1 AngleXU=0 Radius=3.2909
    g21: LineSegment StartX=-13.2904 StartY=-10.9634 StartZ=0 EndX=-16.4692 EndY=-11.8151 EndZ=0
    g22: LineSegment StartX=-16.4692 StartY=-11.8151 StartZ=0 EndX=-17.3209 EndY=-14.9939 EndZ=0
    g23: LineSegment StartX=-17.3209 StartY=-14.9939 StartZ=0 EndX=-14.9939 EndY=-17.3209 EndZ=0
    g24: LineSegment StartX=-14.9939 StartY=-17.3209 StartZ=0 EndX=-11.8151 EndY=-16.4692 EndZ=0
    g25: LineSegment StartX=-11.8151 StartY=-16.4692 StartZ=0 EndX=-10.9634 EndY=-13.2904 EndZ=0
    g26: LineSegment StartX=-10.9634 StartY=-13.2904 StartZ=0 EndX=-13.2904 EndY=-10.9634 EndZ=0
    g27: Circle [constr] CenterX=-14.1421 CenterY=-14.1421 CenterZ=0 NormalX=0 NormalY=0 NormalZ=1 AngleXU=0 Radius=3.2909
    g28: LineSegment StartX=16.4692 StartY=-11.8151 StartZ=0 EndX=13.2904 EndY=-10.9634 EndZ=0
    g29: LineSegment StartX=13.2904 StartY=-10.9634 StartZ=0 EndX=10.9634 EndY=-13.2904 EndZ=0
    g30: LineSegment StartX=10.9634 StartY=-13.2904 StartZ=0 EndX=11.8151 EndY=-16.4692 EndZ=0
    g31: LineSegment StartX=11.8151 StartY=-16.4692 StartZ=0 EndX=14.9939 EndY=-17.3209 EndZ=0
    g32: LineSegment StartX=14.9939 StartY=-17.3209 StartZ=0 EndX=17.3209 EndY=-14.9939 EndZ=0
    g33: LineSegment StartX=17.3209 StartY=-14.9939 StartZ=0 EndX=16.4692 EndY=-11.8151 EndZ=0
    g34: Circle [constr] CenterX=14.1421 CenterY=-14.1421 CenterZ=0 NormalX=0 NormalY=0 NormalZ=1 AngleXU=0 Radius=3.2909
  constraints (84):
    c: Coincident(g0,g-1)
    c: Radius(g0) = 20
    c: PointOnObject(g1,g0)
    c: PointOnObject(g1,g0)
    c: PointOnObject(g2,g0)
    c: PointOnObject(g2,g0)
    c: PointOnObject(g-1,g2)
    c: PointOnObject(g-1,g1)
    c: Perpendicular(g1,g2)
    c: Coincident(g3,g4)
    c: Coincident(g4,g5)
    c: Coincident(g5,g6)
    c: Coincident(g6,g3)
    c: Horizontal(g3)
    c: Horizontal(g5)
    c: Vertical(g4)
    c: Vertical(g6)
    c: Coincident(g3,g1)
    c: Coincident(g4,g1)
    c: Equal(g3,g4)
    c: Coincident(g7,g8)
    c: Coincident(g8,g9)
    c: Coincident(g9,g10)
    c: Coincident(g10,g11)
    c: Coincident(g11,g12)
    c: Coincident(g12,g7)
    c: Equal(g7, g8-g12) x5
    c: PointOnObject(g7,g13)
    c: PointOnObject(g8,g13)
    c: PointOnObject(g9,g13)
    c: PointOnObject(g10,g13)
    c: PointOnObject(g11,g13)
    c: PointOnObject(g12,g13)
    c: Coincident(g13,g1)
    c: Coincident(g14,g15)
    c: Coincident(g15,g16)
    c: Coincident(g16,g17)
    c: Coincident(g17,g18)
    c: Coincident(g18,g19)
    c: Coincident(g19,g14)
    c: Equal(g14, g15-g19) x5
    c: PointOnObject(g14,g20)
    c: PointOnObject(g15,g20)
    c: PointOnObject(g16,g20)
    c: PointOnObject(g17,g20)
    c: PointOnObject(g18,g20)
    c: PointOnObject(g19,g20)
    c: Coincident(g20,g2)
    c: Coincident(g21,g22)
    c: Coincident(g22,g23)
    c: Coincident(g23,g24)
    c: Coincident(g24,g25)
    c: Coincident(g25,g26)
    c: Coincident(g26,g21)
    c: Equal(g21, g22-g26) x5
    c: PointOnObject(g21,g27)
    c: PointOnObject(g22,g27)
    c: PointOnObject(g23,g27)
    c: PointOnObject(g24,g27)
    c: PointOnObject(g25,g27)
    c: PointOnObject(g26,g27)
    c: Coincident(g27,g2)
    c: Perpendicular(g1,g11)
    c: Perpendicular(g2,g16)
    c: Perpendicular(g2,g26)
    c: Coincident(g28,g29)
    c: Coincident(g29,g30)
    c: Coincident(g30,g31)
    c: Coincident(g31,g32)
    c: Coincident(g32,g33)
    c: Coincident(g33,g28)
    c: Equal(g28, g29-g33) x5
    c: PointOnObject(g28,g34)
    c: PointOnObject(g29,g34)
    c: PointOnObject(g30,g34)
    c: PointOnObject(g31,g34)
    c: PointOnObject(g32,g34)
    c: PointOnObject(g33,g34)
    c: Coincident(g34,g1)
    c: Perpendicular(g1,g29)
    c: Equal(g20,g13)
    c: Equal(g13,g27)
    c: Equal(g27,g34)
    c: Distance(g15,g14) = 5.7
FEATURE [PartDesign::Pocket] Pocket409  label="Nutholes Servohorn Cap001"
  BaseFeature = -> Pocket386
  Length = 2.5
  Length2 = 100
  Profile = -> Sketch976
  Type = 0
FEATURE [Sketcher::SketchObject] Sketch966
  MapMode = 5
  Placement = pos=(0,-28.25,0) rot=(1,0,0;1.5708rad)
  Support = -> [Pocket409]
  sketch-geometry (8):
    g0: LineSegment StartX=3.75 StartY=22.9 StartZ=0 EndX=6.75 EndY=22.9 EndZ=0
    g1: LineSegment StartX=6.75 StartY=22.9 StartZ=0 EndX=6.75 EndY=17.1 EndZ=0
    g2: LineSegment StartX=6.75 StartY=17.1 StartZ=0 EndX=3.75 EndY=17.1 EndZ=0
    g3: LineSegment StartX=3.75 StartY=17.1 StartZ=0 EndX=3.75 EndY=22.9 EndZ=0
    g4: LineSegment StartX=3.75 StartY=12.9 StartZ=0 EndX=6.75 EndY=12.9 EndZ=0
    g5: LineSegment StartX=6.75 StartY=12.9 StartZ=0 EndX=6.75 EndY=7.1 EndZ=0
    g6: LineSegment StartX=6.75 StartY=7.1 StartZ=0 EndX=3.75 EndY=7.1 EndZ=0
    g7: LineSegment StartX=3.75 StartY=7.1 StartZ=0 EndX=3.75 EndY=12.9 EndZ=0
  constraints (24):
    c: Coincident(g0,g1)
    c: Coincident(g1,g2)
    c: Coincident(g2,g3)
    c: Coincident(g3,g0)
    c: Horizontal(g0)
    c: Horizontal(g2)
    c: Vertical(g1)
    c: Vertical(g3)
    c: Coincident(g4,g5)
    c: Coincident(g5,g6)
    c: Coincident(g6,g7)
    c: Coincident(g7,g4)
    c: Horizontal(g4)
    c: Horizontal(g6)
    c: Vertical(g5)
    c: Vertical(g7)
    c: Equal(g0,g4)
    c: Equal(g1,g5)
    c: DistanceY(g1,g1) = 5.8
    c: DistanceY(g4,g1) = 4.2
    c: DistanceX(g-1,g5) = 6.75
    c: DistanceX(g0,g0) = 3
    c: Vertical(g4,g1)
    c: DistanceY(g-1,g5) = 7.1
FEATURE [PartDesign::Pocket] Pocket403  label="Nutholes Servo Pocket001"
  BaseFeature = -> Pocket409
  Length = 56.5
  Length2 = 100
  Profile = -> Sketch966
  Type = 0
FEATURE [Sketcher::SketchObject] Sketch970
  MapMode = 5
  Placement = pos=(9.75,0,0) rot=(0.57735,0.57735,0.57735;2.0944rad)
  Support = -> [Pocket403]
  sketch-geometry (4):
    g0: Circle CenterX=-24.25 CenterY=20 CenterZ=0 NormalX=0 NormalY=0 NormalZ=1 AngleXU=0 Radius=1.6
    g1: Circle CenterX=-24.25 CenterY=10 CenterZ=0 NormalX=0 NormalY=0 NormalZ=1 AngleXU=0 Radius=1.6
    g2: Circle CenterX=24.25 CenterY=20 CenterZ=0 NormalX=0 NormalY=0 NormalZ=1 AngleXU=0 Radius=1.6
    g3: Circle CenterX=24.25 CenterY=10 CenterZ=0 NormalX=0 NormalY=0 NormalZ=1 AngleXU=0 Radius=1.6
  constraints (11):
    c: Vertical(g3,g2)
    c: Vertical(g1,g0)
    c: Symmetric(g0,g2,g-2)
    c: Radius(g0) = 1.6
    c: Equal(g0,g1)
    c: Equal(g0,g2)
    c: Equal(g0,g3)
    c: DistanceY(g3,g2) = 10
    c: Horizontal(g1,g3)
    c: DistanceY(g-1,g3) = 10
    c: DistanceX(g0,g2) = 48.5
FEATURE [PartDesign::Pad] Pad445  label="Baseplate020"
  Length = 12
  Length2 = 100
  Profile = -> Sketch963
  Type = 0
FEATURE [Sketcher::SketchObject] Sketch977
  MapMode = 5
  Placement = pos=(0,0,12) rot=(0,0,1;0rad)
  Support = -> [Pad445]
  sketch-geometry (9):
    g0: Circle [constr] CenterX=0 CenterY=0 CenterZ=0 NormalX=0 NormalY=0 NormalZ=1 AngleXU=0 Radius=20
    g1: LineSegment [constr] StartX=-14.1421 StartY=14.1421 StartZ=0 EndX=14.1421 EndY=14.1421 EndZ=0
    g2: LineSegment [constr] StartX=14.1421 StartY=14.1421 StartZ=0 EndX=14.1421 EndY=-14.1421 EndZ=0
    g3: LineSegment [constr] StartX=14.1421 StartY=-14.1421 StartZ=0 EndX=-14.1421 EndY=-14.1421 EndZ=0
    g4: LineSegment [constr] StartX=-14.1421 StartY=-14.1421 StartZ=0 EndX=-14.1421 EndY=14.1421 EndZ=0
    g5: Circle CenterX=-14.1421 CenterY=14.1421 CenterZ=0 NormalX=0 NormalY=0 NormalZ=1 AngleXU=0 Radius=1.6
    g6: Circle CenterX=14.1421 CenterY=14.1421 CenterZ=0 NormalX=0 NormalY=0 NormalZ=1 AngleXU=0 Radius=1.6
    g7: Circle CenterX=14.1421 CenterY=-14.1421 CenterZ=0 NormalX=0 NormalY=0 NormalZ=1 AngleXU=0 Radius=1.6
    g8: Circle CenterX=-14.1421 CenterY=-14.1421 CenterZ=0 NormalX=0 NormalY=0 NormalZ=1 AngleXU=0 Radius=1.6
  constraints (22):
    c: Coincident(g0,g-1)
    c: Radius(g0) = 20
    c: Coincident(g1,g2)
    c: Coincident(g2,g3)
    c: Coincident(g3,g4)
    c: Coincident(g4,g1)
    c: Horizontal(g1)
    c: Horizontal(g3)
    c: Vertical(g2)
    c: Vertical(g4)
    c: PointOnObject(g1,g0)
    c: PointOnObject(g2,g0)
    c: PointOnObject(g1,g0)
    c: Equal(g1,g2)
    c: Coincident(g5,g1)
    c: Coincident(g6,g1)
    c: Coincident(g7,g2)
    c: Coincident(g8,g3)
    c: Equal(g8,g5)
    c: Equal(g5,g6)
    c: Equal(g6,g7)
    c: Radius(g6) = 1.6
FEATURE [PartDesign::Pocket] Pocket405  label="Screwholes Mounting001"
  BaseFeature = -> Pad445
  Length = 12
  Length2 = 100
  Profile = -> Sketch977
  Type = 0
FEATURE [Sketcher::SketchObject] Sketch987
  MapMode = 5
  Placement = pos=(0,0,12) rot=(0,0,1;0rad)
  Support = -> [Pocket405]
  sketch-geometry (1):
    g0: Circle CenterX=0 CenterY=0 CenterZ=0 NormalX=0 NormalY=0 NormalZ=1 AngleXU=0 Radius=16.5
  constraints (2):
    c: Coincident(g0,g-1)
    c: Radius(g0) = 16.5
FEATURE [PartDesign::Pocket] Pocket412  label="Accesshole001"
  BaseFeature = -> Pocket405
  Length = 7
  Length2 = 100
  Profile = -> Sketch987
  Type = 0
FEATURE [Sketcher::SketchObject] Sketch969
  MapMode = 5
  Placement = pos=(0,0,5) rot=(0,0,1;0rad)
  Support = -> [Pocket412]
  sketch-geometry (1):
    g0: Circle CenterX=0 CenterY=0 CenterZ=0 NormalX=0 NormalY=0 NormalZ=1 AngleXU=0 Radius=6.15
  constraints (2):
    c: Coincident(g0,g-1)
    c: Radius(g0) = 6.15
FEATURE [PartDesign::Pocket] Pocket408  label="Servohole001"
  BaseFeature = -> Pocket412
  Length = 5
  Length2 = 100
  Profile = -> Sketch969
  Type = 0
FEATURE [Sketcher::SketchObject] Sketch990
  MapMode = 5
  Placement = pos=(0,0,5) rot=(0,0,1;0rad)
  Support = -> [Pocket408]
  sketch-geometry (32):
    g0: LineSegment [constr] StartX=3.75 StartY=6.49519 StartZ=0 EndX=-3.75 EndY=6.49519 EndZ=0
    g1: LineSegment [constr] StartX=-3.75 StartY=6.49519 StartZ=0 EndX=-7.5 EndY=9e-16 EndZ=0
    g2: LineSegment [constr] StartX=-7.5 StartY=9e-16 StartZ=0 EndX=-3.75 EndY=-6.49519 EndZ=0
    g3: LineSegment [constr] StartX=-3.75 StartY=-6.49519 StartZ=0 EndX=3.75 EndY=-6.49519 EndZ=0
    g4: LineSegment [constr] StartX=3.75 StartY=-6.49519 StartZ=0 EndX=7.5 EndY=0 EndZ=0
    g5: LineSegment [constr] StartX=7.5 StartY=0 StartZ=0 EndX=3.75 EndY=6.49519 EndZ=0
    g6: Circle [constr] CenterX=0 CenterY=0 CenterZ=0 NormalX=0 NormalY=0 NormalZ=1 AngleXU=0 Radius=7.5
    g7: LineSegment [constr] StartX=0 StartY=13.5 StartZ=0 EndX=-11.6913 EndY=6.75 EndZ=0
    g8: LineSegment [constr] StartX=-11.6913 StartY=6.75 StartZ=0 EndX=-11.6913 EndY=-6.75 EndZ=0
    g9: LineSegment [constr] StartX=-11.6913 StartY=-6.75 StartZ=0 EndX=0 EndY=-13.5 EndZ=0
    g10: LineSegment [constr] StartX=-5e-16 StartY=-13.5 StartZ=0 EndX=11.6913 EndY=-6.75 EndZ=0
    g11: LineSegment [constr] StartX=11.6913 StartY=-6.75 StartZ=0 EndX=11.6913 EndY=6.75 EndZ=0
    g12: LineSegment [constr] StartX=11.6913 StartY=6.75 StartZ=0 EndX=0 EndY=13.5 EndZ=0
    g13: Circle [constr] CenterX=0 CenterY=0 CenterZ=0 NormalX=0 NormalY=0 NormalZ=1 AngleXU=0 Radius=13.5
    g14: ArcOfCircle CenterX=0 CenterY=13.5 CenterZ=0 NormalX=0 NormalY=0 NormalZ=1 AngleXU=0 Radius=2.6 StartAngle=0.15815 EndAngle=2.98344
    g15: ArcOfCircle CenterX=11.6913 CenterY=6.75 CenterZ=0 NormalX=0 NormalY=0 NormalZ=1 AngleXU=0 Radius=2.6 StartAngle=5.39414 EndAngle=8.21943
    g16: ArcOfCircle CenterX=11.6913 CenterY=-6.75 CenterZ=0 NormalX=0 NormalY=0 NormalZ=1 AngleXU=0 Radius=2.6 StartAngle=4.34694 EndAngle=7.17223
    g17: ArcOfCircle CenterX=-5e-16 CenterY=-13.5 CenterZ=0 NormalX=0 NormalY=0 NormalZ=1 AngleXU=0 Radius=2.6 StartAngle=3.29974 EndAngle=6.12503
    g18: ArcOfCircle CenterX=-11.6913 CenterY=-6.75 CenterZ=0 NormalX=0 NormalY=0 NormalZ=1 AngleXU=0 Radius=2.6 StartAngle=2.25255 EndAngle=5.07784
    g19: ArcOfCircle CenterX=-11.6913 CenterY=6.75 CenterZ=0 NormalX=0 NormalY=0 NormalZ=1 AngleXU=0 Radius=2.6 StartAngle=1.20535 EndAngle=4.03064
    g20: LineSegment StartX=-2.56755 StartY=13.9095 StartZ=0 EndX=-3.75 EndY=6.49519 EndZ=0
    g21: LineSegment StartX=-3.75 StartY=6.49519 StartZ=0 EndX=-10.7622 EndY=9.17831 EndZ=0
    g22: LineSegment StartX=2.56755 StartY=13.9095 StartZ=0 EndX=3.75 EndY=6.49519 EndZ=0
    g23: LineSegment StartX=3.75 StartY=6.49519 StartZ=0 EndX=10.7622 EndY=9.17831 EndZ=0
    g24: LineSegment StartX=13.3297 StartY=4.73117 StartZ=0 EndX=7.5 EndY=0 EndZ=0
    g25: LineSegment StartX=7.5 StartY=0 StartZ=0 EndX=13.3297 EndY=-4.73117 EndZ=0
    g26: LineSegment StartX=10.7622 StartY=-9.17831 StartZ=0 EndX=3.75 EndY=-6.49519 EndZ=0
    g27: LineSegment StartX=3.75 StartY=-6.49519 StartZ=0 EndX=2.56755 EndY=-13.9095 EndZ=0
    g28: LineSegment StartX=-2.56755 StartY=-13.9095 StartZ=0 EndX=-3.75 EndY=-6.49519 EndZ=0
    g29: LineSegment StartX=-3.75 StartY=-6.49519 StartZ=0 EndX=-10.7622 EndY=-9.17831 EndZ=0
    g30: LineSegment StartX=-13.3297 StartY=-4.73117 StartZ=0 EndX=-7.5 EndY=9e-16 EndZ=0
    g31: LineSegment StartX=-7.5 StartY=9e-16 StartZ=0 EndX=-13.3297 EndY=4.73117 EndZ=0
  constraints (68):
    c: Coincident(g0,g1)
    c: Coincident(g1,g2)
    c: Coincident(g2,g3)
    c: Coincident(g3,g4)
    c: Coincident(g4,g5)
    c: Coincident(g5,g0)
    c: Equal(g0, g1-g5) x5
    c: PointOnObject(g0,g6)
    c: PointOnObject(g1,g6)
    c: PointOnObject(g2,g6)
    c: PointOnObject(g3,g6)
    c: PointOnObject(g4,g6)
    c: PointOnObject(g5,g6)
    c: Coincident(g6,g-1)
    c: Coincident(g7,g8)
    c: Coincident(g8,g9)
    c: Coincident(g9,g10)
    c: Coincident(g10,g11)
    c: Coincident(g11,g12)
    c: Coincident(g12,g7)
    c: Equal(g7, g8-g12) x5
    c: PointOnObject(g7,g13)
    c: PointOnObject(g8,g13)
    c: PointOnObject(g9,g13)
    c: PointOnObject(g10,g13)
    c: PointOnObject(g11,g13)
    c: PointOnObject(g12,g13)
    c: Coincident(g13,g-1)
    c: Horizontal(g0)
    c: Vertical(g8)
    c: Radius(g6) = 7.5
    c: Radius(g13) = 13.5
    c: Coincident(g14,g7)
    c: Coincident(g15,g11)
    c: Coincident(g16,g10)
    c: Coincident(g17,g9)
    c: Coincident(g18,g8)
    c: Coincident(g19,g7)
    c: Coincident(g20,g0)
    c: Coincident(g21,g20)
    c: Coincident(g22,g0)
    c: Coincident(g23,g22)
    c: Coincident(g24,g4)
    c: Coincident(g25,g24)
    c: Coincident(g26,g3)
    c: Coincident(g27,g26)
    c: Coincident(g28,g2)
    c: Coincident(g29,g28)
    c: Coincident(g31,g30)
    c: Tangent(g21,g19) = -1.5708
    c: Tangent(g20,g14) = -1.5708
    c: Tangent(g22,g14) = 1.5708
    c: Tangent(g23,g15) = 1.5708
    c: Tangent(g24,g15) = 1.5708
    c: Tangent(g25,g16) = 1.5708
    c: Tangent(g26,g16) = 1.5708
    c: Tangent(g27,g17) = 1.5708
    c: Tangent(g28,g17) = 1.5708
    c: Tangent(g29,g18) = 1.5708
    c: Tangent(g30,g18) = 1.5708
    c: Tangent(g31,g19) = 1.5708
    c: Radius(g14) = 2.6
    c: Equal(g14,g15)
    c: Equal(g15,g16)
    c: Equal(g16,g17)
    c: Equal(g17,g18)
    c: Equal(g18,g19)
    c: Coincident(g30,g1)
FEATURE [PartDesign::Pocket] Pocket413  label="Servohorn009"
  BaseFeature = -> Pocket408
  Length = 2
  Length2 = 100
  Profile = -> Sketch990
  Type = 0
FEATURE [PartDesign::Fillet] Fillet089  label="Smooth Servohorn Corners001"
  Base = -> Pocket413 [Edge81,Edge87,Edge82,Edge88,Edge93,Edge94]
  BaseFeature = -> Pocket413
  Radius = 1
FEATURE [Sketcher::SketchObject] Sketch989
  MapMode = 5
  Placement = pos=(0,0,3) rot=(0,0,1;0rad)
  Support = -> [Fillet089]
  sketch-geometry (13):
    g0: LineSegment [constr] StartX=0 StartY=10.5 StartZ=0 EndX=-9.09327 EndY=5.25 EndZ=0
    g1: LineSegment [constr] StartX=-9.09327 StartY=5.25 StartZ=0 EndX=-9.09327 EndY=-5.25 EndZ=0
    g2: LineSegment [constr] StartX=-9.09327 StartY=-5.25 StartZ=0 EndX=0 EndY=-10.5 EndZ=0
    g3: LineSegment [constr] StartX=0 StartY=-10.5 StartZ=0 EndX=9.09327 EndY=-5.25 EndZ=0
    g4: LineSegment [constr] StartX=9.09327 StartY=-5.25 StartZ=0 EndX=9.09327 EndY=5.25 EndZ=0
    g5: LineSegment [constr] StartX=9.09327 StartY=5.25 StartZ=0 EndX=0 EndY=10.5 EndZ=0
    g6: Circle [constr] CenterX=0 CenterY=0 CenterZ=0 NormalX=0 NormalY=0 NormalZ=1 AngleXU=0 Radius=10.5
    g7: Circle CenterX=0 CenterY=10.5 CenterZ=0 NormalX=0 NormalY=0 NormalZ=1 AngleXU=0 Radius=0.95
    g8: Circle CenterX=9.09327 CenterY=5.25 CenterZ=0 NormalX=0 NormalY=0 NormalZ=1 AngleXU=0 Radius=0.95
    g9: Circle CenterX=9.09327 CenterY=-5.25 CenterZ=0 NormalX=0 NormalY=0 NormalZ=1 AngleXU=0 Radius=0.95
    g10: Circle CenterX=0 CenterY=-10.5 CenterZ=0 NormalX=0 NormalY=0 NormalZ=1 AngleXU=0 Radius=0.95
    g11: Circle CenterX=-9.09327 CenterY=-5.25 CenterZ=0 NormalX=0 NormalY=0 NormalZ=1 AngleXU=0 Radius=0.95
    g12: Circle CenterX=-9.09327 CenterY=5.25 CenterZ=0 NormalX=0 NormalY=0 NormalZ=1 AngleXU=0 Radius=0.95
  constraints (24):
    c: Coincident(g0,g1)
    c: Coincident(g1,g2)
    c: Coincident(g2,g3)
    c: Coincident(g3,g4)
    c: Coincident(g4,g5)
    c: Coincident(g5,g0)
    c: Equal(g0, g1-g5) x5
    c: PointOnObject(g0,g6)
    c: PointOnObject(g1,g6)
    c: PointOnObject(g2,g6)
    c: PointOnObject(g3,g6)
    c: PointOnObject(g4,g6)
    c: PointOnObject(g5,g6)
    c: Coincident(g6,g-1)
    c: PointOnObject(g5,g-2)
    c: Radius(g6) = 10.5
    c: Coincident(g7,g0)
    c: Coincident(g8,g4)
    c: Coincident(g9,g3)
    c: Coincident(g10,g2)
    c: Coincident(g11,g1)
    c: Coincident(g12,g0)
    c: Radius(g12) = 0.95
    c: Equal(g12, g7-g11) x5
FEATURE [PartDesign::Pocket] Pocket400  label="Screwholes Servohorn001"
  BaseFeature = -> Fillet089
  Length = 3
  Length2 = 100
  Profile = -> Sketch989
  Type = 0
FEATURE [Sketcher::SketchObject] Sketch978
  MapMode = 5
  Placement = pos=(0,0,0) rot=(1,0,0;3.14159rad)
  Support = -> [Pocket400]
  sketch-geometry (10):
    g0: Circle [constr] CenterX=0 CenterY=0 CenterZ=0 NormalX=0 NormalY=0 NormalZ=1 AngleXU=0 Radius=20
    g1: LineSegment [constr] StartX=-14.1421 StartY=14.1421 StartZ=0 EndX=14.1421 EndY=14.1421 EndZ=0
    g2: LineSegment [constr] StartX=14.1421 StartY=14.1421 StartZ=0 EndX=14.1421 EndY=-14.1421 EndZ=0
    g3: LineSegment [constr] StartX=14.1421 StartY=-14.1421 StartZ=0 EndX=-14.1421 EndY=-14.1421 EndZ=0
    g4: LineSegment [constr] StartX=-14.1421 StartY=-14.1421 StartZ=0 EndX=-14.1421 EndY=14.1421 EndZ=0
    g5: Circle CenterX=-14.1421 CenterY=14.1421 CenterZ=0 NormalX=0 NormalY=0 NormalZ=1 AngleXU=0 Radius=1.2e-15
    g6: Circle CenterX=14.1421 CenterY=14.1421 CenterZ=0 NormalX=0 NormalY=0 NormalZ=1 AngleXU=0 Radius=2.85
    g7: Circle CenterX=14.1421 CenterY=-14.1421 CenterZ=0 NormalX=0 NormalY=0 NormalZ=1 AngleXU=0 Radius=2.85
    g8: Circle CenterX=-14.1421 CenterY=14.1421 CenterZ=0 NormalX=0 NormalY=0 NormalZ=1 AngleXU=0 Radius=2.85
    g9: Circle CenterX=-14.1421 CenterY=-14.1421 CenterZ=0 NormalX=0 NormalY=0 NormalZ=1 AngleXU=0 Radius=2.85
  constraints (24):
    c: Coincident(g0,g-1)
    c: Radius(g0) = 20
    c: Coincident(g1,g2)
    c: Coincident(g2,g3)
    c: Coincident(g3,g4)
    c: Coincident(g4,g1)
    c: Horizontal(g1)
    c: Horizontal(g3)
    c: Vertical(g2)
    c: Vertical(g4)
    c: PointOnObject(g1,g0)
    c: PointOnObject(g2,g0)
    c: PointOnObject(g1,g0)
    c: Equal(g1,g2)
    c: Coincident(g5,g1)
    c: Tangent(g5,g0)
    c: Coincident(g6,g1)
    c: Coincident(g7,g2)
    c: Coincident(g8,g5)
    c: Coincident(g9,g3)
    c: Equal(g9,g8)
    c: Equal(g8,g6)
    c: Equal(g6,g7)
    c: Radius(g6) = 2.85
FEATURE [PartDesign::Pocket] Pocket406  label="Screwheads Mounting001"
  BaseFeature = -> Pocket400
  Length = 8
  Length2 = 100
  Profile = -> Sketch978
  Type = 0
FEATURE [PartDesign::Chamfer] Chamfer160  label="Screwheads Bottom Chamfer001"
  Base = -> Pocket406 [Edge140,Edge139,Edge138,Edge137]
  BaseFeature = -> Pocket406
  Size = 1.2
FEATURE [PartDesign::Body] Body245  label="Shoulder_Joint_Servohorn_Cap001"
  Group = -> [Sketch963,Pad445,Sketch977,Pocket405,Sketch987,Pocket412,Sketch969,Pocket408,Sketch990,Pocket413,Fillet089,Sketch989,Pocket400,Sketch978,Pocket406,Chamfer160]
  Origin = -> Origin260
  Tip = -> Chamfer160
FEATURE [PartDesign::Pocket] Pocket414  label="Screwholes Servo Pocket001"
  BaseFeature = -> Pocket403
  Length = 18
  Length2 = 100
  Profile = -> Sketch970
  Type = 0
FEATURE [Sketcher::SketchObject] Sketch980
  MapMode = 5
  Placement = pos=(-18.75,0,0) rot=(0.57735,0.57735,0.57735;2.0944rad)
  Support = -> [Pocket414]
  sketch-geometry (1):
    g0: Circle CenterX=10 CenterY=15 CenterZ=0 NormalX=0 NormalY=0 NormalZ=1 AngleXU=0 Radius=0.95
  constraints (3):
    c: DistanceY(g-1,g0) = 15
    c: DistanceX(g-1,g0) = 10
    c: Radius(g0) = 0.95
FEATURE [PartDesign::Pocket] Pocket407  label="Screwhole Ball Bearing Pin001"
  BaseFeature = -> Pocket414
  Length = 3
  Length2 = 100
  Profile = -> Sketch980
  Type = 0
FEATURE [Sketcher::SketchObject] Sketch973
  MapMode = 5
  Placement = pos=(-18.75,0,0) rot=(0.57735,0.57735,0.57735;2.0944rad)
  Support = -> [Pocket407]
  sketch-geometry (7):
    g0: LineSegment StartX=12.05 StartY=13.8164 StartZ=0 EndX=12.05 EndY=16.1836 EndZ=0
    g1: LineSegment StartX=12.05 StartY=16.1836 StartZ=0 EndX=10 EndY=17.3671 EndZ=0
    g2: LineSegment StartX=10 StartY=17.3671 StartZ=0 EndX=7.95 EndY=16.1836 EndZ=0
    g3: LineSegment StartX=7.95 StartY=16.1836 StartZ=0 EndX=7.95 EndY=13.8164 EndZ=0
    g4: LineSegment StartX=7.95 StartY=13.8164 StartZ=0 EndX=10 EndY=12.6329 EndZ=0
    g5: LineSegment StartX=10 StartY=12.6329 StartZ=0 EndX=12.05 EndY=13.8164 EndZ=0
    g6: Circle [constr] CenterX=10 CenterY=15 CenterZ=0 NormalX=0 NormalY=0 NormalZ=1 AngleXU=0 Radius=2.36714
  constraints (17):
    c: Coincident(g0,g1)
    c: Coincident(g1,g2)
    c: Coincident(g2,g3)
    c: Coincident(g3,g4)
    c: Coincident(g4,g5)
    c: Coincident(g5,g0)
    c: Equal(g0, g1-g5) x5
    c: PointOnObject(g0,g6)
    c: PointOnObject(g1,g6)
    c: PointOnObject(g2,g6)
    c: PointOnObject(g3,g6)
    c: PointOnObject(g4,g6)
    c: PointOnObject(g5,g6)
    c: Vertical(g3)
    c: DistanceX(g-1,g6) = 10
    c: DistanceY(g-1,g6) = 15
    c: Distance(g0,g4) = 4.1
FEATURE [PartDesign::Pocket] Pocket411  label="Nuthole Ball Bearing Pin001"
  BaseFeature = -> Pocket407
  Length = 1.5
  Length2 = 100
  Profile = -> Sketch973
  Type = 0
FEATURE [Sketcher::SketchObject] Sketch962
  MapMode = 5
  Placement = pos=(0,28.25,0) rot=(0,0.707107,0.707107;3.14159rad)
  Support = -> [Pocket411]
  sketch-geometry (4):
    g0: LineSegment StartX=9.25 StartY=25 StartZ=0 EndX=14.25 EndY=25 EndZ=0
    g1: LineSegment StartX=14.25 StartY=25 StartZ=0 EndX=14.25 EndY=11.5 EndZ=0
    g2: ArcOfCircle CenterX=11.75 CenterY=11.5 CenterZ=0 NormalX=0 NormalY=0 NormalZ=1 AngleXU=0 Radius=2.5 StartAngle=3.14159 EndAngle=6.28319
    g3: LineSegment StartX=9.25 StartY=11.5 StartZ=0 EndX=9.25 EndY=25 EndZ=0
  constraints (11):
    c: Horizontal(g0)
    c: Coincident(g0,g1)
    c: Vertical(g1)
    c: Tangent(g1,g2) = 1.5708
    c: Tangent(g2,g3) = 1.5708
    c: Coincident(g3,g0)
    c: DistanceX(g0,g0) = 5
    c: Vertical(g3)
    c: DistanceX(g-1,g2) = 11.75
    c: DistanceY(g-1,g2) = 11.5
    c: DistanceY(g1,g1) = 13.5
FEATURE [PartDesign::Pocket] Pocket402  label="Servocable007"
  BaseFeature = -> Pocket411
  Length = 8
  Length2 = 100
  Profile = -> Sketch962
  Type = 0
FEATURE [PartDesign::Fillet] Fillet093  label="Smooth Servo Pocket Edges001"
  Base = -> Pocket402 [Edge62,Edge137,Edge61,Edge146,Edge60]
  BaseFeature = -> Pocket402
  Radius = 1
FEATURE [PartDesign::Fillet] Fillet122  label="Smooth Servocable Edges004"
  Base = -> Fillet093 [Edge10,Edge165]
  BaseFeature = -> Fillet093
  Radius = 2.5
FEATURE [PartDesign::Body] Body249  label="Shoulder_Joint_Servomount001"
  Group = -> [Sketch975,Pad442,Pad435,Sketch981,Pocket397,Sketch974,Pocket398,Sketch959,Pocket386,Sketch976,Pocket409,Sketch966,Pocket403,Sketch970,Pocket414,Sketch980,Pocket407,Sketch973,Pocket411,Sketch962,Pocket402,Fillet093,Fillet122]
  Origin = -> Origin310
  Tip = -> Fillet122
FEATURE [Sketcher::SketchObject] Sketch992
  MapMode = 5
  Support = -> [XY_Plane350]
  sketch-geometry (1):
    g0: Circle CenterX=0 CenterY=0 CenterZ=0 NormalX=0 NormalY=0 NormalZ=1 AngleXU=0 Radius=1.9
  constraints (2):
    c: Coincident(g0,g-1)
    c: Radius(g0) = 1.9
FEATURE [PartDesign::Pad] Pad410  label="M3x8 Head047"
  Length = 2
  Length2 = 100
  Profile = -> Sketch992
  Type = 0
FEATURE [Sketcher::SketchObject] Sketch993
  MapMode = 5
  Support = -> [XY_Plane332]
  sketch-geometry (1):
    g0: Circle CenterX=0 CenterY=0 CenterZ=0 NormalX=0 NormalY=0 NormalZ=1 AngleXU=0 Radius=2.75
  constraints (2):
    c: Coincident(g0,g-1)
    c: Radius(g0) = 2.75
FEATURE [PartDesign::Pad] Pad421  label="M3x8 Head052"
  Length = 3
  Length2 = 100
  Profile = -> Sketch993
  Type = 0
FEATURE [Sketcher::SketchObject] Sketch994
  MapMode = 5
  Support = -> [XY_Plane346]
FEATURE [Sketcher::SketchObject] Sketch995
  MapMode = 5
  Support = -> [XY_Plane362]
  sketch-geometry (8):
    g0: LineSegment StartX=0 StartY=3.17543 StartZ=0 EndX=-2.75 EndY=1.58771 EndZ=0
    g1: LineSegment StartX=-2.75 StartY=1.58771 StartZ=0 EndX=-2.75 EndY=-1.58771 EndZ=0
    g2: LineSegment StartX=-2.75 StartY=-1.58771 StartZ=0 EndX=0 EndY=-3.17543 EndZ=0
    g3: LineSegment StartX=0 StartY=-3.17543 StartZ=0 EndX=2.75 EndY=-1.58771 EndZ=0
    g4: LineSegment StartX=2.75 StartY=-1.58771 StartZ=0 EndX=2.75 EndY=1.58771 EndZ=0
    g5: LineSegment StartX=2.75 StartY=1.58771 StartZ=0 EndX=0 EndY=3.17543 EndZ=0
    g6: Circle [constr] CenterX=0 CenterY=0 CenterZ=0 NormalX=0 NormalY=0 NormalZ=1 AngleXU=0 Radius=3.17543
    g7: Circle CenterX=0 CenterY=0 CenterZ=0 NormalX=0 NormalY=0 NormalZ=1 AngleXU=0 Radius=1.5
  constraints (18):
    c: Coincident(g0,g1)
    c: Coincident(g1,g2)
    c: Coincident(g2,g3)
    c: Coincident(g3,g4)
    c: Coincident(g4,g5)
    c: Coincident(g5,g0)
    c: Equal(g0, g1-g5) x5
    c: PointOnObject(g0,g6)
    c: PointOnObject(g1,g6)
    c: PointOnObject(g2,g6)
    c: PointOnObject(g3,g6)
    c: PointOnObject(g4,g6)
    c: PointOnObject(g5,g6)
    c: Coincident(g6,g-1)
    c: PointOnObject(g5,g-2)
    c: DistanceX(g0,g4) = 5.5
    c: Coincident(g7,g-1)
    c: Radius(g7) = 1.5
FEATURE [PartDesign::Pad] Pad446  label="M3 Nut Primitive086"
  Length = 1.2
  Length2 = 1.2
  Profile = -> Sketch995
  Type = 4
FEATURE [Sketcher::SketchObject] Sketch991
  ExternalGeometry = -> [Pad446]
  MapMode = 5
  Placement = pos=(0,0,0) rot=(0.57735,0.57735,0.57735;2.0944rad)
  Support = -> [YZ_Plane355]
  sketch-geometry (6):
    g0: LineSegment StartX=-2.67543 StartY=1.2 StartZ=0 EndX=-3.67543 EndY=1.2 EndZ=0
    g1: LineSegment StartX=-3.67543 StartY=1.2 StartZ=0 EndX=-3.67543 EndY=-1.2 EndZ=0
    g2: LineSegment StartX=-3.67543 StartY=-1.2 StartZ=0 EndX=-2.67543 EndY=-1.2 EndZ=0
    g3: LineSegment StartX=-2.67543 StartY=-1.2 StartZ=0 EndX=-3.17543 EndY=-1 EndZ=0
    g4: LineSegment StartX=-3.17543 StartY=-1 StartZ=0 EndX=-3.17543 EndY=1 EndZ=0
    g5: LineSegment StartX=-3.17543 StartY=1 StartZ=0 EndX=-2.67543 EndY=1.2 EndZ=0
  constraints (15):
    c: Horizontal(g0)
    c: Coincident(g0,g1)
    c: Coincident(g1,g2)
    c: Coincident(g2,g3)
    c: Coincident(g3,g4)
    c: Coincident(g4,g5)
    c: Coincident(g5,g0)
    c: Symmetric(g4,g3,g-1)
    c: Symmetric(g0,g2,g-1)
    c: Symmetric(g1,g0,g-1)
    c: DistanceX(g0,g4) = 0.5
    c: DistanceY(g3,g4) = 2
    c: DistanceY(g1,g0) = 2.4
    c: PointOnObject(g3,g-3)
    c: DistanceX(g4,g0) = 0.5
FEATURE [PartDesign::Groove] Groove086  label="M3 Nut Smooth082"
  Angle = 360
  Axis = (-2e-16,3e-16,1)
  Base = (0,0,0)
  BaseFeature = -> Pad446
  Profile = -> Sketch991
  ReferenceAxis = -> Sketch991 [V_Axis]
  Reversed = true
FEATURE [PartDesign::Chamfer] Chamfer216  label="M3 Nut Smooth Hole091"
  Base = -> Groove086 [Edge24,Edge23]
  BaseFeature = -> Groove086
  Size = 0.2
FEATURE [PartDesign::Body] Body234  label="M3 Nut044"
  Group = -> [Sketch995,Pad446,Sketch991,Groove086,Chamfer216]
  Origin = -> Origin292
  Placement = pos=(-14.15,-14.15,3.5) rot=(0,0,-1;0.261799rad)
  Tip = -> Chamfer216
FEATURE [Sketcher::SketchObject] Sketch997
  MapMode = 5
  Support = -> [XY_Plane359]
  sketch-geometry (1):
    g0: Circle CenterX=0 CenterY=0 CenterZ=0 NormalX=0 NormalY=0 NormalZ=1 AngleXU=0 Radius=2.75
  constraints (2):
    c: Coincident(g0,g-1)
    c: Radius(g0) = 2.75
FEATURE [PartDesign::Pad] Pad414  label="M3x8 Head049"
  Length = 3
  Length2 = 100
  Profile = -> Sketch997
  Type = 0
FEATURE [Sketcher::SketchObject] Sketch998
  MapMode = 5
  Support = -> [XY_Plane346]
FEATURE [Sketcher::SketchObject] Sketch999
  MapMode = 5
  Support = -> [XY_Plane354]
  sketch-geometry (8):
    g0: LineSegment StartX=0 StartY=3.17543 StartZ=0 EndX=-2.75 EndY=1.58771 EndZ=0
    g1: LineSegment StartX=-2.75 StartY=1.58771 StartZ=0 EndX=-2.75 EndY=-1.58771 EndZ=0
    g2: LineSegment StartX=-2.75 StartY=-1.58771 StartZ=0 EndX=0 EndY=-3.17543 EndZ=0
    g3: LineSegment StartX=0 StartY=-3.17543 StartZ=0 EndX=2.75 EndY=-1.58771 EndZ=0
    g4: LineSegment StartX=2.75 StartY=-1.58771 StartZ=0 EndX=2.75 EndY=1.58771 EndZ=0
    g5: LineSegment StartX=2.75 StartY=1.58771 StartZ=0 EndX=0 EndY=3.17543 EndZ=0
    g6: Circle [constr] CenterX=0 CenterY=0 CenterZ=0 NormalX=0 NormalY=0 NormalZ=1 AngleXU=0 Radius=3.17543
    g7: Circle CenterX=0 CenterY=0 CenterZ=0 NormalX=0 NormalY=0 NormalZ=1 AngleXU=0 Radius=1.5
  constraints (18):
    c: Coincident(g0,g1)
    c: Coincident(g1,g2)
    c: Coincident(g2,g3)
    c: Coincident(g3,g4)
    c: Coincident(g4,g5)
    c: Coincident(g5,g0)
    c: Equal(g0, g1-g5) x5
    c: PointOnObject(g0,g6)
    c: PointOnObject(g1,g6)
    c: PointOnObject(g2,g6)
    c: PointOnObject(g3,g6)
    c: PointOnObject(g4,g6)
    c: PointOnObject(g5,g6)
    c: Coincident(g6,g-1)
    c: PointOnObject(g5,g-2)
    c: DistanceX(g0,g4) = 5.5
    c: Coincident(g7,g-1)
    c: Radius(g7) = 1.5
FEATURE [PartDesign::Pad] Pad434  label="M3 Nut Primitive083"
  Length = 1.2
  Length2 = 1.2
  Profile = -> Sketch999
  Type = 4
FEATURE [Sketcher::SketchObject] Sketch1001
  MapMode = 5
  Support = -> [XY_Plane331]
FEATURE [Sketcher::SketchObject] Sketch1002
  ExternalGeometry = -> [Pad434]
  MapMode = 5
  Placement = pos=(0,0,0) rot=(0.57735,0.57735,0.57735;2.0944rad)
  Support = -> [YZ_Plane350]
  sketch-geometry (6):
    g0: LineSegment StartX=-2.67543 StartY=1.2 StartZ=0 EndX=-3.67543 EndY=1.2 EndZ=0
    g1: LineSegment StartX=-3.67543 StartY=1.2 StartZ=0 EndX=-3.67543 EndY=-1.2 EndZ=0
    g2: LineSegment StartX=-3.67543 StartY=-1.2 StartZ=0 EndX=-2.67543 EndY=-1.2 EndZ=0
    g3: LineSegment StartX=-2.67543 StartY=-1.2 StartZ=0 EndX=-3.17543 EndY=-1 EndZ=0
    g4: LineSegment StartX=-3.17543 StartY=-1 StartZ=0 EndX=-3.17543 EndY=1 EndZ=0
    g5: LineSegment StartX=-3.17543 StartY=1 StartZ=0 EndX=-2.67543 EndY=1.2 EndZ=0
  constraints (15):
    c: Horizontal(g0)
    c: Coincident(g0,g1)
    c: Coincident(g1,g2)
    c: Coincident(g2,g3)
    c: Coincident(g3,g4)
    c: Coincident(g4,g5)
    c: Coincident(g5,g0)
    c: Symmetric(g4,g3,g-1)
    c: Symmetric(g0,g2,g-1)
    c: Symmetric(g1,g0,g-1)
    c: DistanceX(g0,g4) = 0.5
    c: DistanceY(g3,g4) = 2
    c: DistanceY(g1,g0) = 2.4
    c: PointOnObject(g3,g-3)
    c: DistanceX(g4,g0) = 0.5
FEATURE [PartDesign::Groove] Groove085  label="M3 Nut Smooth081"
  Angle = 360
  Axis = (-2e-16,3e-16,1)
  Base = (0,0,0)
  BaseFeature = -> Pad434
  Profile = -> Sketch1002
  ReferenceAxis = -> Sketch1002 [V_Axis]
  Reversed = true
FEATURE [PartDesign::Chamfer] Chamfer215  label="M3 Nut Smooth Hole090"
  Base = -> Groove085 [Edge24,Edge23]
  BaseFeature = -> Groove085
  Size = 0.2
FEATURE [PartDesign::Body] Body236  label="M3 Nut045"
  Group = -> [Sketch999,Pad434,Sketch1002,Groove085,Chamfer215]
  Origin = -> Origin302
  Placement = pos=(-14.15,14.15,3.5) rot=(0,0,1;0.261799rad)
  Tip = -> Chamfer215
FEATURE [Sketcher::SketchObject] Sketch1004
  MapMode = 5
  Support = -> [XY_Plane344]
  sketch-geometry (8):
    g0: LineSegment StartX=0 StartY=3.17543 StartZ=0 EndX=-2.75 EndY=1.58771 EndZ=0
    g1: LineSegment StartX=-2.75 StartY=1.58771 StartZ=0 EndX=-2.75 EndY=-1.58771 EndZ=0
    g2: LineSegment StartX=-2.75 StartY=-1.58771 StartZ=0 EndX=0 EndY=-3.17543 EndZ=0
    g3: LineSegment StartX=0 StartY=-3.17543 StartZ=0 EndX=2.75 EndY=-1.58771 EndZ=0
    g4: LineSegment StartX=2.75 StartY=-1.58771 StartZ=0 EndX=2.75 EndY=1.58771 EndZ=0
    g5: LineSegment StartX=2.75 StartY=1.58771 StartZ=0 EndX=0 EndY=3.17543 EndZ=0
    g6: Circle [constr] CenterX=0 CenterY=0 CenterZ=0 NormalX=0 NormalY=0 NormalZ=1 AngleXU=0 Radius=3.17543
    g7: Circle CenterX=0 CenterY=0 CenterZ=0 NormalX=0 NormalY=0 NormalZ=1 AngleXU=0 Radius=1.5
  constraints (18):
    c: Coincident(g0,g1)
    c: Coincident(g1,g2)
    c: Coincident(g2,g3)
    c: Coincident(g3,g4)
    c: Coincident(g4,g5)
    c: Coincident(g5,g0)
    c: Equal(g0, g1-g5) x5
    c: PointOnObject(g0,g6)
    c: PointOnObject(g1,g6)
    c: PointOnObject(g2,g6)
    c: PointOnObject(g3,g6)
    c: PointOnObject(g4,g6)
    c: PointOnObject(g5,g6)
    c: Coincident(g6,g-1)
    c: PointOnObject(g5,g-2)
    c: DistanceX(g0,g4) = 5.5
    c: Coincident(g7,g-1)
    c: Radius(g7) = 1.5
FEATURE [PartDesign::Pad] Pad447  label="M3 Nut Primitive087"
  Length = 1.2
  Length2 = 1.2
  Profile = -> Sketch1004
  Type = 4
FEATURE [Sketcher::SketchObject] Sketch1006
  ExternalGeometry = -> [Pad447]
  MapMode = 5
  Placement = pos=(0,0,0) rot=(0.57735,0.57735,0.57735;2.0944rad)
  Support = -> [YZ_Plane357]
  sketch-geometry (6):
    g0: LineSegment StartX=-2.67543 StartY=1.2 StartZ=0 EndX=-3.67543 EndY=1.2 EndZ=0
    g1: LineSegment StartX=-3.67543 StartY=1.2 StartZ=0 EndX=-3.67543 EndY=-1.2 EndZ=0
    g2: LineSegment StartX=-3.67543 StartY=-1.2 StartZ=0 EndX=-2.67543 EndY=-1.2 EndZ=0
    g3: LineSegment StartX=-2.67543 StartY=-1.2 StartZ=0 EndX=-3.17543 EndY=-1 EndZ=0
    g4: LineSegment StartX=-3.17543 StartY=-1 StartZ=0 EndX=-3.17543 EndY=1 EndZ=0
    g5: LineSegment StartX=-3.17543 StartY=1 StartZ=0 EndX=-2.67543 EndY=1.2 EndZ=0
  constraints (15):
    c: Horizontal(g0)
    c: Coincident(g0,g1)
    c: Coincident(g1,g2)
    c: Coincident(g2,g3)
    c: Coincident(g3,g4)
    c: Coincident(g4,g5)
    c: Coincident(g5,g0)
    c: Symmetric(g4,g3,g-1)
    c: Symmetric(g0,g2,g-1)
    c: Symmetric(g1,g0,g-1)
    c: DistanceX(g0,g4) = 0.5
    c: DistanceY(g3,g4) = 2
    c: DistanceY(g1,g0) = 2.4
    c: PointOnObject(g3,g-3)
    c: DistanceX(g4,g0) = 0.5
FEATURE [PartDesign::Groove] Groove091  label="M3 Nut Smooth087"
  Angle = 360
  Axis = (-2e-16,3e-16,1)
  Base = (0,0,0)
  BaseFeature = -> Pad447
  Profile = -> Sketch1006
  ReferenceAxis = -> Sketch1006 [V_Axis]
  Reversed = true
FEATURE [PartDesign::Chamfer] Chamfer152  label="M3 Nut Smooth Hole062"
  Base = -> Groove091 [Edge24,Edge23]
  BaseFeature = -> Groove091
  Size = 0.2
FEATURE [PartDesign::Body] Body239  label="M3 Nut046"
  Group = -> [Sketch1004,Pad447,Sketch1006,Groove091,Chamfer152]
  Origin = -> Origin275
  Placement = pos=(14.15,-14.15,3.5) rot=(0,0,1;0.261799rad)
  Tip = -> Chamfer152
FEATURE [Sketcher::SketchObject] Sketch1009
  MapMode = 5
  Support = -> [XY_Plane358]
  sketch-geometry (8):
    g0: LineSegment StartX=0 StartY=3.17543 StartZ=0 EndX=-2.75 EndY=1.58771 EndZ=0
    g1: LineSegment StartX=-2.75 StartY=1.58771 StartZ=0 EndX=-2.75 EndY=-1.58771 EndZ=0
    g2: LineSegment StartX=-2.75 StartY=-1.58771 StartZ=0 EndX=0 EndY=-3.17543 EndZ=0
    g3: LineSegment StartX=0 StartY=-3.17543 StartZ=0 EndX=2.75 EndY=-1.58771 EndZ=0
    g4: LineSegment StartX=2.75 StartY=-1.58771 StartZ=0 EndX=2.75 EndY=1.58771 EndZ=0
    g5: LineSegment StartX=2.75 StartY=1.58771 StartZ=0 EndX=0 EndY=3.17543 EndZ=0
    g6: Circle [constr] CenterX=0 CenterY=0 CenterZ=0 NormalX=0 NormalY=0 NormalZ=1 AngleXU=0 Radius=3.17543
    g7: Circle CenterX=0 CenterY=0 CenterZ=0 NormalX=0 NormalY=0 NormalZ=1 AngleXU=0 Radius=1.5
  constraints (18):
    c: Coincident(g0,g1)
    c: Coincident(g1,g2)
    c: Coincident(g2,g3)
    c: Coincident(g3,g4)
    c: Coincident(g4,g5)
    c: Coincident(g5,g0)
    c: Equal(g0, g1-g5) x5
    c: PointOnObject(g0,g6)
    c: PointOnObject(g1,g6)
    c: PointOnObject(g2,g6)
    c: PointOnObject(g3,g6)
    c: PointOnObject(g4,g6)
    c: PointOnObject(g5,g6)
    c: Coincident(g6,g-1)
    c: PointOnObject(g5,g-2)
    c: DistanceX(g0,g4) = 5.5
    c: Coincident(g7,g-1)
    c: Radius(g7) = 1.5
FEATURE [PartDesign::Pad] Pad441  label="M3 Nut Primitive085"
  Length = 1.2
  Length2 = 1.2
  Profile = -> Sketch1009
  Type = 4
FEATURE [Sketcher::SketchObject] Sketch1012
  ExternalGeometry = -> [Pad441]
  MapMode = 5
  Placement = pos=(0,0,0) rot=(0.57735,0.57735,0.57735;2.0944rad)
  Support = -> [YZ_Plane346]
  sketch-geometry (6):
    g0: LineSegment StartX=-2.67543 StartY=1.2 StartZ=0 EndX=-3.67543 EndY=1.2 EndZ=0
    g1: LineSegment StartX=-3.67543 StartY=1.2 StartZ=0 EndX=-3.67543 EndY=-1.2 EndZ=0
    g2: LineSegment StartX=-3.67543 StartY=-1.2 StartZ=0 EndX=-2.67543 EndY=-1.2 EndZ=0
    g3: LineSegment StartX=-2.67543 StartY=-1.2 StartZ=0 EndX=-3.17543 EndY=-1 EndZ=0
    g4: LineSegment StartX=-3.17543 StartY=-1 StartZ=0 EndX=-3.17543 EndY=1 EndZ=0
    g5: LineSegment StartX=-3.17543 StartY=1 StartZ=0 EndX=-2.67543 EndY=1.2 EndZ=0
  constraints (15):
    c: Horizontal(g0)
    c: Coincident(g0,g1)
    c: Coincident(g1,g2)
    c: Coincident(g2,g3)
    c: Coincident(g3,g4)
    c: Coincident(g4,g5)
    c: Coincident(g5,g0)
    c: Symmetric(g4,g3,g-1)
    c: Symmetric(g0,g2,g-1)
    c: Symmetric(g1,g0,g-1)
    c: DistanceX(g0,g4) = 0.5
    c: DistanceY(g3,g4) = 2
    c: DistanceY(g1,g0) = 2.4
    c: PointOnObject(g3,g-3)
    c: DistanceX(g4,g0) = 0.5
FEATURE [PartDesign::Groove] Groove090  label="M3 Nut Smooth086"
  Angle = 360
  Axis = (-2e-16,3e-16,1)
  Base = (0,0,0)
  BaseFeature = -> Pad441
  Profile = -> Sketch1012
  ReferenceAxis = -> Sketch1012 [V_Axis]
  Reversed = true
FEATURE [PartDesign::Chamfer] Chamfer163  label="M3 Nut Smooth Hole067"
  Base = -> Groove090 [Edge24,Edge23]
  BaseFeature = -> Groove090
  Size = 0.2
FEATURE [PartDesign::Body] Body243  label="M3 Nut047"
  Group = -> [Sketch1009,Pad441,Sketch1012,Groove090,Chamfer163]
  Origin = -> Origin270
  Placement = pos=(14.15,14.15,3.5) rot=(0,0,-1;0.261799rad)
  Tip = -> Chamfer163
FEATURE [App::Part] Part074  label="Shouldercap Nuts001"
  Group = -> [Body243,Body236,Body239,Body234]
  Origin = -> Origin262
FEATURE [Sketcher::SketchObject] Sketch1015
  MapMode = 5
  Support = -> [XY_Plane351]
  sketch-geometry (1):
    g0: Circle CenterX=0 CenterY=0 CenterZ=0 NormalX=0 NormalY=0 NormalZ=1 AngleXU=0 Radius=2.75
  constraints (2):
    c: Coincident(g0,g-1)
    c: Radius(g0) = 2.75
FEATURE [PartDesign::Pad] Pad426  label="M3x8 Head054"
  Length = 3
  Length2 = 100
  Profile = -> Sketch1015
  Type = 0
FEATURE [Sketcher::SketchObject] Sketch1011
  MapMode = 5
  Placement = pos=(0,0,3) rot=(0,0,1;0rad)
  Support = -> [Pad426]
  sketch-geometry (1):
    g0: Circle CenterX=0 CenterY=0 CenterZ=0 NormalX=0 NormalY=0 NormalZ=1 AngleXU=0 Radius=1.5
  constraints (2):
    c: Coincident(g0,g-1)
    c: Radius(g0) = 1.5
FEATURE [PartDesign::Pad] Pad436  label="M3x8 Thread054"
  BaseFeature = -> Pad426
  Length = 8
  Length2 = 100
  Profile = -> Sketch1011
  Type = 0
FEATURE [Sketcher::SketchObject] Sketch1010
  MapMode = 5
  Placement = pos=(0,0,0) rot=(1,0,0;3.14159rad)
  Support = -> [Pad436]
  sketch-geometry (7):
    g0: LineSegment StartX=1.275 StartY=0.736122 StartZ=0 EndX=0 EndY=1.47224 EndZ=0
    g1: LineSegment StartX=0 StartY=1.47224 StartZ=0 EndX=-1.275 EndY=0.736122 EndZ=0
    g2: LineSegment StartX=-1.275 StartY=0.736122 StartZ=0 EndX=-1.275 EndY=-0.736122 EndZ=0
    g3: LineSegment StartX=-1.275 StartY=-0.736122 StartZ=0 EndX=1.34766e-11 EndY=-1.47224 EndZ=0
    g4: LineSegment StartX=1.34766e-11 StartY=-1.47224 StartZ=0 EndX=1.275 EndY=-0.736122 EndZ=0
    g5: LineSegment StartX=1.275 StartY=-0.736122 StartZ=0 EndX=1.275 EndY=0.736122 EndZ=0
    g6: Circle [constr] CenterX=0 CenterY=0 CenterZ=0 NormalX=0 NormalY=0 NormalZ=1 AngleXU=0 Radius=1.47224
  constraints (16):
    c: Coincident(g0,g1)
    c: Coincident(g1,g2)
    c: Coincident(g2,g3)
    c: Coincident(g3,g4)
    c: Coincident(g4,g5)
    c: Coincident(g5,g0)
    c: Equal(g0, g1-g5) x5
    c: PointOnObject(g0,g6)
    c: PointOnObject(g1,g6)
    c: PointOnObject(g2,g6)
    c: PointOnObject(g3,g6)
    c: PointOnObject(g4,g6)
    c: PointOnObject(g5,g6)
    c: Coincident(g6,g-1)
    c: PointOnObject(g0,g-2)
    c: DistanceX(g1,g0) = 2.55
FEATURE [PartDesign::Pocket] Pocket404  label="M3x8 Wrench055"
  BaseFeature = -> Pad436
  Length = 1.3
  Length2 = 100
  Profile = -> Sketch1010
  Type = 0
FEATURE [PartDesign::Chamfer] Chamfer158  label="M3x8 Smooth043"
  Base = -> Pocket404 [Face11,Edge2,Edge24,Edge3]
  BaseFeature = -> Pocket404
  Size = 0.2
FEATURE [PartDesign::Body] Body237  label="M3x057"
  Group = -> [Sketch1015,Pad426,Sketch1011,Pad436,Sketch1010,Pocket404,Chamfer158]
  Origin = -> Origin315
  Placement = pos=(-14.15,-14.15,-6) rot=(0,0,1;0rad)
  Tip = -> Chamfer158
FEATURE [Sketcher::SketchObject] Sketch1018
  MapMode = 5
  Placement = pos=(0,0,3) rot=(0,0,1;0rad)
  Support = -> [Pad414]
  sketch-geometry (1):
    g0: Circle CenterX=0 CenterY=0 CenterZ=0 NormalX=0 NormalY=0 NormalZ=1 AngleXU=0 Radius=1.5
  constraints (2):
    c: Coincident(g0,g-1)
    c: Radius(g0) = 1.5
FEATURE [PartDesign::Pad] Pad417  label="M3x8 Thread048"
  BaseFeature = -> Pad414
  Length = 8
  Length2 = 100
  Profile = -> Sketch1018
  Type = 0
FEATURE [Sketcher::SketchObject] Sketch1014
  MapMode = 5
  Placement = pos=(0,0,0) rot=(1,0,0;3.14159rad)
  Support = -> [Pad417]
  sketch-geometry (7):
    g0: LineSegment StartX=1.275 StartY=0.736122 StartZ=0 EndX=0 EndY=1.47224 EndZ=0
    g1: LineSegment StartX=0 StartY=1.47224 StartZ=0 EndX=-1.275 EndY=0.736122 EndZ=0
    g2: LineSegment StartX=-1.275 StartY=0.736122 StartZ=0 EndX=-1.275 EndY=-0.736122 EndZ=0
    g3: LineSegment StartX=-1.275 StartY=-0.736122 StartZ=0 EndX=1.34766e-11 EndY=-1.47224 EndZ=0
    g4: LineSegment StartX=1.34766e-11 StartY=-1.47224 StartZ=0 EndX=1.275 EndY=-0.736122 EndZ=0
    g5: LineSegment StartX=1.275 StartY=-0.736122 StartZ=0 EndX=1.275 EndY=0.736122 EndZ=0
    g6: Circle [constr] CenterX=0 CenterY=0 CenterZ=0 NormalX=0 NormalY=0 NormalZ=1 AngleXU=0 Radius=1.47224
  constraints (16):
    c: Coincident(g0,g1)
    c: Coincident(g1,g2)
    c: Coincident(g2,g3)
    c: Coincident(g3,g4)
    c: Coincident(g4,g5)
    c: Coincident(g5,g0)
    c: Equal(g0, g1-g5) x5
    c: PointOnObject(g0,g6)
    c: PointOnObject(g1,g6)
    c: PointOnObject(g2,g6)
    c: PointOnObject(g3,g6)
    c: PointOnObject(g4,g6)
    c: PointOnObject(g5,g6)
    c: Coincident(g6,g-1)
    c: PointOnObject(g0,g-2)
    c: DistanceX(g1,g0) = 2.55
FEATURE [PartDesign::Pocket] Pocket387  label="M3x8 Wrench045"
  BaseFeature = -> Pad417
  Length = 1.3
  Length2 = 100
  Profile = -> Sketch1014
  Type = 0
FEATURE [PartDesign::Chamfer] Chamfer141  label="M3x8 Smooth039"
  Base = -> Pocket387 [Face11,Edge2,Edge24,Edge3]
  BaseFeature = -> Pocket387
  Size = 0.2
FEATURE [PartDesign::Body] Body242  label="M3x058"
  Group = -> [Sketch997,Pad414,Sketch1018,Pad417,Sketch1014,Pocket387,Chamfer141]
  Origin = -> Origin296
  Placement = pos=(14.15,-14.15,-6) rot=(0,0,1;0rad)
  Tip = -> Chamfer141
FEATURE [Sketcher::SketchObject] Sketch1022
  MapMode = 5
  Placement = pos=(0,0,3) rot=(0,0,1;0rad)
  Support = -> [Pad421]
  sketch-geometry (1):
    g0: Circle CenterX=0 CenterY=0 CenterZ=0 NormalX=0 NormalY=0 NormalZ=1 AngleXU=0 Radius=1.5
  constraints (2):
    c: Coincident(g0,g-1)
    c: Radius(g0) = 1.5
FEATURE [PartDesign::Pad] Pad443  label="M3x8 Thread055"
  BaseFeature = -> Pad421
  Length = 8
  Length2 = 100
  Profile = -> Sketch1022
  Type = 0
FEATURE [Sketcher::SketchObject] Sketch1003
  MapMode = 5
  Placement = pos=(0,0,0) rot=(1,0,0;3.14159rad)
  Support = -> [Pad443]
  sketch-geometry (7):
    g0: LineSegment StartX=1.275 StartY=0.736122 StartZ=0 EndX=0 EndY=1.47224 EndZ=0
    g1: LineSegment StartX=0 StartY=1.47224 StartZ=0 EndX=-1.275 EndY=0.736122 EndZ=0
    g2: LineSegment StartX=-1.275 StartY=0.736122 StartZ=0 EndX=-1.275 EndY=-0.736122 EndZ=0
    g3: LineSegment StartX=-1.275 StartY=-0.736122 StartZ=0 EndX=1.34766e-11 EndY=-1.47224 EndZ=0
    g4: LineSegment StartX=1.34766e-11 StartY=-1.47224 StartZ=0 EndX=1.275 EndY=-0.736122 EndZ=0
    g5: LineSegment StartX=1.275 StartY=-0.736122 StartZ=0 EndX=1.275 EndY=0.736122 EndZ=0
    g6: Circle [constr] CenterX=0 CenterY=0 CenterZ=0 NormalX=0 NormalY=0 NormalZ=1 AngleXU=0 Radius=1.47224
  constraints (16):
    c: Coincident(g0,g1)
    c: Coincident(g1,g2)
    c: Coincident(g2,g3)
    c: Coincident(g3,g4)
    c: Coincident(g4,g5)
    c: Coincident(g5,g0)
    c: Equal(g0, g1-g5) x5
    c: PointOnObject(g0,g6)
    c: PointOnObject(g1,g6)
    c: PointOnObject(g2,g6)
    c: PointOnObject(g3,g6)
    c: PointOnObject(g4,g6)
    c: PointOnObject(g5,g6)
    c: Coincident(g6,g-1)
    c: PointOnObject(g0,g-2)
    c: DistanceX(g1,g0) = 2.55
FEATURE [PartDesign::Pocket] Pocket401  label="M3x8 Wrench054"
  BaseFeature = -> Pad443
  Length = 1.3
  Length2 = 100
  Profile = -> Sketch1003
  Type = 0
FEATURE [PartDesign::Chamfer] Chamfer165  label="M3x8 Smooth046"
  Base = -> Pocket401 [Face11,Edge2,Edge24,Edge3]
  BaseFeature = -> Pocket401
  Size = 0.2
FEATURE [PartDesign::Body] Body208  label="M3x047"
  Group = -> [Sketch993,Pad421,Sketch1022,Pad443,Sketch1003,Pocket401,Chamfer165]
  Origin = -> Origin300
  Placement = pos=(-14.15,14.15,-6) rot=(0,0,1;0rad)
  Tip = -> Chamfer165
FEATURE [Sketcher::SketchObject] Sketch1024
  MapMode = 5
  Placement = pos=(0,0,0) rot=(0.57735,0.57735,0.57735;2.0944rad)
  Support = -> [YZ_Plane310]
  sketch-geometry (1):
    g0: LineSegment StartX=0 StartY=0 StartZ=0 EndX=0 EndY=190 EndZ=0
  constraints (3):
    c: Coincident(g0,g-1)
    c: Vertical(g0)
    c: DistanceY(g0,g0) = 190
FEATURE [Sketcher::SketchObject] Sketch1026
  ExternalGeometry = -> [Pad429]
  MapMode = 5
  Placement = pos=(0,0,0) rot=(0.57735,0.57735,0.57735;2.0944rad)
  Support = -> [YZ_Plane320]
  sketch-geometry (6):
    g0: LineSegment StartX=-1.9594 StartY=0.6 StartZ=0 EndX=-2.8094 EndY=0.6 EndZ=0
    g1: LineSegment StartX=-2.8094 StartY=0.6 StartZ=0 EndX=-2.8094 EndY=-0.6 EndZ=0
    g2: LineSegment StartX=-2.8094 StartY=-0.6 StartZ=0 EndX=-1.9594 EndY=-0.6 EndZ=0
    g3: LineSegment StartX=-1.9594 StartY=-0.6 StartZ=0 EndX=-2.3094 EndY=-0.4 EndZ=0
    g4: LineSegment StartX=-2.3094 StartY=-0.4 StartZ=0 EndX=-2.3094 EndY=0.4 EndZ=0
    g5: LineSegment StartX=-2.3094 StartY=0.4 StartZ=0 EndX=-1.9594 EndY=0.6 EndZ=0
  constraints (15):
    c: Horizontal(g0)
    c: Coincident(g0,g1)
    c: Coincident(g1,g2)
    c: Coincident(g2,g3)
    c: Coincident(g3,g4)
    c: Coincident(g4,g5)
    c: Coincident(g5,g0)
    c: Symmetric(g4,g3,g-1)
    c: Symmetric(g0,g2,g-1)
    c: Symmetric(g1,g0,g-1)
    c: DistanceX(g0,g4) = 0.5
    c: DistanceY(g3,g4) = 0.8
    c: DistanceY(g1,g0) = 1.2
    c: PointOnObject(g3,g-3)
    c: DistanceX(g4,g0) = 0.35
FEATURE [PartDesign::Groove] Groove083  label="M3 Nut Smooth079"
  Angle = 360
  Axis = (-2e-16,3e-16,1)
  Base = (0,0,0)
  BaseFeature = -> Pad429
  Profile = -> Sketch1026
  ReferenceAxis = -> Sketch1026 [V_Axis]
  Reversed = true
FEATURE [PartDesign::Chamfer] Chamfer159  label="M3 Nut Smooth Hole066"
  Base = -> Groove083 [Edge24,Edge23]
  BaseFeature = -> Groove083
  Size = 0.2
FEATURE [PartDesign::Body] Body207  label="M2 Nut033"
  Group = -> [Sketch985,Pad429,Sketch1026,Groove083,Chamfer159,Sketch965,Sketch967]
  Origin = -> Origin297
  Placement = pos=(0,0,2.75) rot=(0,0,1;0rad)
  Tip = -> Chamfer159
FEATURE [Sketcher::SketchObject] Sketch1027
  MapMode = 5
  Support = -> [XY_Plane379]
  sketch-geometry (1):
    g0: Circle CenterX=0 CenterY=0 CenterZ=0 NormalX=0 NormalY=0 NormalZ=1 AngleXU=0 Radius=2.75
  constraints (2):
    c: Coincident(g0,g-1)
    c: Radius(g0) = 2.75
FEATURE [PartDesign::Pad] Pad439  label="M3x8 Head056"
  Length = 3
  Length2 = 100
  Profile = -> Sketch1027
  Type = 0
FEATURE [Sketcher::SketchObject] Sketch1016
  MapMode = 5
  Placement = pos=(0,0,3) rot=(0,0,1;0rad)
  Support = -> [Pad439]
  sketch-geometry (1):
    g0: Circle CenterX=0 CenterY=0 CenterZ=0 NormalX=0 NormalY=0 NormalZ=1 AngleXU=0 Radius=1.5
  constraints (2):
    c: Coincident(g0,g-1)
    c: Radius(g0) = 1.5
FEATURE [PartDesign::Pad] Pad444  label="M3x8 Thread056"
  BaseFeature = -> Pad439
  Length = 8
  Length2 = 100
  Profile = -> Sketch1016
  Type = 0
FEATURE [Sketcher::SketchObject] Sketch1028
  MapMode = 5
  Placement = pos=(0,0,0) rot=(1,0,0;3.14159rad)
  Support = -> [Pad444]
  sketch-geometry (7):
    g0: LineSegment StartX=1.275 StartY=0.736122 StartZ=0 EndX=0 EndY=1.47224 EndZ=0
    g1: LineSegment StartX=0 StartY=1.47224 StartZ=0 EndX=-1.275 EndY=0.736122 EndZ=0
    g2: LineSegment StartX=-1.275 StartY=0.736122 StartZ=0 EndX=-1.275 EndY=-0.736122 EndZ=0
    g3: LineSegment StartX=-1.275 StartY=-0.736122 StartZ=0 EndX=1.34766e-11 EndY=-1.47224 EndZ=0
    g4: LineSegment StartX=1.34766e-11 StartY=-1.47224 StartZ=0 EndX=1.275 EndY=-0.736122 EndZ=0
    g5: LineSegment StartX=1.275 StartY=-0.736122 StartZ=0 EndX=1.275 EndY=0.736122 EndZ=0
    g6: Circle [constr] CenterX=0 CenterY=0 CenterZ=0 NormalX=0 NormalY=0 NormalZ=1 AngleXU=0 Radius=1.47224
  constraints (16):
    c: Coincident(g0,g1)
    c: Coincident(g1,g2)
    c: Coincident(g2,g3)
    c: Coincident(g3,g4)
    c: Coincident(g4,g5)
    c: Coincident(g5,g0)
    c: Equal(g0, g1-g5) x5
    c: PointOnObject(g0,g6)
    c: PointOnObject(g1,g6)
    c: PointOnObject(g2,g6)
    c: PointOnObject(g3,g6)
    c: PointOnObject(g4,g6)
    c: PointOnObject(g5,g6)
    c: Coincident(g6,g-1)
    c: PointOnObject(g0,g-2)
    c: DistanceX(g1,g0) = 2.55
FEATURE [PartDesign::Pocket] Pocket410  label="M3x8 Wrench056"
  BaseFeature = -> Pad444
  Length = 1.3
  Length2 = 100
  Profile = -> Sketch1028
  Type = 0
FEATURE [PartDesign::Chamfer] Chamfer151  label="M3x8 Smooth041"
  Base = -> Pocket410 [Face11,Edge2,Edge24,Edge3]
  BaseFeature = -> Pocket410
  Size = 0.2
FEATURE [PartDesign::Body] Body254  label="M3x059"
  Group = -> [Sketch1027,Pad439,Sketch1016,Pad444,Sketch1028,Pocket410,Chamfer151,Sketch1024]
  Origin = -> Origin276
  Placement = pos=(-5.2,-40,200.6) rot=(-1,0,0;1.5708rad)
  Tip = -> Chamfer151
FEATURE [Sketcher::SketchObject] Sketch1033
  MapMode = 5
  Support = -> [XY_Plane312]
  sketch-geometry (4):
    g0: LineSegment StartX=-10 StartY=20.15 StartZ=0 EndX=10 EndY=20.15 EndZ=0
    g1: LineSegment StartX=10 StartY=20.15 StartZ=0 EndX=10 EndY=-20.15 EndZ=0
    g2: LineSegment StartX=10 StartY=-20.15 StartZ=0 EndX=-10 EndY=-20.15 EndZ=0
    g3: LineSegment StartX=-10 StartY=-20.15 StartZ=0 EndX=-10 EndY=20.15 EndZ=0
  constraints (10):
    c: Coincident(g0,g1)
    c: Coincident(g1,g2)
    c: Coincident(g2,g3)
    c: Coincident(g3,g0)
    c: Horizontal(g2)
    c: Vertical(g3)
    c: DistanceX(g0,g0) = 20
    c: DistanceY(g1,g1) = 40.3
    c: Symmetric(g0,g1,g-1)
    c: Symmetric(g0,g0,g-2)
FEATURE [PartDesign::Pad] Pad464  label="Baseblock009"
  Length = 26.6
  Length2 = 100
  Profile = -> Sketch1033
  Type = 0
FEATURE [Sketcher::SketchObject] Sketch1029
  MapMode = 5
  Placement = pos=(0,0,26.6) rot=(0,0,1;0rad)
  Support = -> [Pad464]
  sketch-geometry (4):
    g0: LineSegment StartX=-10 StartY=-26.8 StartZ=0 EndX=10 EndY=-26.8 EndZ=0
    g1: LineSegment StartX=10 StartY=-26.8 StartZ=0 EndX=10 EndY=26.8 EndZ=0
    g2: LineSegment StartX=10 StartY=26.8 StartZ=0 EndX=-10 EndY=26.8 EndZ=0
    g3: LineSegment StartX=-10 StartY=26.8 StartZ=0 EndX=-10 EndY=-26.8 EndZ=0
  constraints (10):
    c: Coincident(g0,g1)
    c: Coincident(g1,g2)
    c: Coincident(g2,g3)
    c: Coincident(g3,g0)
    c: Horizontal(g0)
    c: Vertical(g3)
    c: Symmetric(g1,g2,g-2)
    c: Symmetric(g1,g0,g-1)
    c: DistanceX(g2,g2) = 20
    c: DistanceY(g1,g1) = 53.6
FEATURE [PartDesign::Pad] Pad463
  BaseFeature = -> Pad464
  Length = 2.5
  Length2 = 100
  Profile = -> Sketch1029
  Type = 0
FEATURE [Sketcher::SketchObject] Sketch1017
  MapMode = 5
  Placement = pos=(0,0,29.1) rot=(0,0,1;0rad)
  Support = -> [Pad463]
  sketch-geometry (4):
    g0: LineSegment StartX=-10 StartY=-20.15 StartZ=0 EndX=10 EndY=-20.15 EndZ=0
    g1: LineSegment StartX=10 StartY=-20.15 StartZ=0 EndX=10 EndY=20.15 EndZ=0
    g2: LineSegment StartX=10 StartY=20.15 StartZ=0 EndX=-10 EndY=20.15 EndZ=0
    g3: LineSegment StartX=-10 StartY=20.15 StartZ=0 EndX=-10 EndY=-20.15 EndZ=0
  constraints (10):
    c: Coincident(g0,g1)
    c: Coincident(g1,g2)
    c: Coincident(g2,g3)
    c: Coincident(g3,g0)
    c: Horizontal(g0)
    c: Vertical(g3)
    c: Symmetric(g1,g2,g-2)
    c: Symmetric(g1,g0,g-1)
    c: DistanceX(g2,g2) = 20
    c: DistanceY(g1,g1) = 40.3
FEATURE [PartDesign::Pad] Pad454
  BaseFeature = -> Pad463
  Length = 6
  Length2 = 100
  Profile = -> Sketch1017
  Type = 0
FEATURE [Sketcher::SketchObject] Sketch1030
  ExternalGeometry = -> [Pad454]
  MapMode = 5
  Placement = pos=(0,0,35.1) rot=(0,0,1;0rad)
  Support = -> [Pad454]
  sketch-geometry (7):
    g0: ArcOfCircle CenterX=-3e-16 CenterY=10.15 CenterZ=0 NormalX=0 NormalY=0 NormalZ=1 AngleXU=0 Radius=9.5 StartAngle=5.9573 EndAngle=9.75066
    g1: LineSegment StartX=-9 StartY=7.10862 StartZ=0 EndX=-9 EndY=-14.15 EndZ=0
    g2: LineSegment StartX=-9 StartY=-14.15 StartZ=0 EndX=-5 EndY=-14.15 EndZ=0
    g3: LineSegment StartX=5 StartY=-14.15 StartZ=0 EndX=9 EndY=-14.15 EndZ=0
    g4: LineSegment StartX=9 StartY=-14.15 StartZ=0 EndX=9 EndY=7.10862 EndZ=0
    g5: ArcOfCircle CenterX=-3e-16 CenterY=-10.4 CenterZ=0 NormalX=0 NormalY=0 NormalZ=1 AngleXU=0 Radius=6.25 StartAngle=3.78509 EndAngle=5.63968
    g6: LineSegment [constr] StartX=0 StartY=-20.15 StartZ=0 EndX=0 EndY=-16.65 EndZ=0
  constraints (22):
    c: Symmetric(g0,g0,g-2)
    c: Coincident(g1,g0)
    c: Vertical(g1)
    c: Coincident(g2,g1)
    c: Horizontal(g2)
    c: Horizontal(g3)
    c: Coincident(g4,g3)
    c: Coincident(g4,g0)
    c: Vertical(g4)
    c: Symmetric(g2,g3,g-2)
    c: Coincident(g5,g2)
    c: Coincident(g5,g3)
    c: DistanceY(g-3,g3) = 6
    c: DistanceY(g0,g-4) = 10
    c: Radius(g0) = 9.5
    c: DistanceX(g0,g0) = 18
    c: PointOnObject(g6,g-3)
    c: PointOnObject(g6,g5)
    c: Vertical(g6)
    c: DistanceY(g6,g6) = 3.5
    c: DistanceX(g2,g3) = 10
    c: PointOnObject(g6,g-2)
FEATURE [PartDesign::Pad] Pad440
  BaseFeature = -> Pad454
  Length = 2.5
  Length2 = 100
  Profile = -> Sketch1030
  Type = 0
FEATURE [Sketcher::SketchObject] Sketch1034
  MapMode = 5
  Placement = pos=(0,0,0) rot=(1,0,0;1.5708rad)
  Support = -> [XZ_Plane353]
  sketch-geometry (1):
    g0: Circle CenterX=0 CenterY=4 CenterZ=0 NormalX=0 NormalY=0 NormalZ=1 AngleXU=0 Radius=0.75
  constraints (3):
    c: PointOnObject(g0,g-2)
    c: Radius(g0) = 0.75
    c: DistanceY(g-1,g0) = 4
FEATURE [PartDesign::Pad] Pad467
  Length = 10
  Length2 = 100
  Placement = pos=(0,0,0) rot=(1,0,0;1.5708rad)
  Profile = -> Sketch1034
  Reversed = true
  Type = 0
FEATURE [PartDesign::Body] Body271  label="red wire008"
  Group = -> [Sketch1034,Pad467]
  Origin = -> Origin278
  Placement = pos=(0,25.15,0) rot=(0,0,1;0rad)
  Tip = -> Pad467
FEATURE [Sketcher::SketchObject] Sketch1036
  MapMode = 5
  Support = -> [XY_Plane363]
  sketch-geometry (8):
    g0: LineSegment StartX=0 StartY=3.17543 StartZ=0 EndX=-2.75 EndY=1.58771 EndZ=0
    g1: LineSegment StartX=-2.75 StartY=1.58771 StartZ=0 EndX=-2.75 EndY=-1.58771 EndZ=0
    g2: LineSegment StartX=-2.75 StartY=-1.58771 StartZ=0 EndX=0 EndY=-3.17543 EndZ=0
    g3: LineSegment StartX=0 StartY=-3.17543 StartZ=0 EndX=2.75 EndY=-1.58771 EndZ=0
    g4: LineSegment StartX=2.75 StartY=-1.58771 StartZ=0 EndX=2.75 EndY=1.58771 EndZ=0
    g5: LineSegment StartX=2.75 StartY=1.58771 StartZ=0 EndX=0 EndY=3.17543 EndZ=0
    g6: Circle [constr] CenterX=0 CenterY=0 CenterZ=0 NormalX=0 NormalY=0 NormalZ=1 AngleXU=0 Radius=3.17543
    g7: Circle CenterX=0 CenterY=0 CenterZ=0 NormalX=0 NormalY=0 NormalZ=1 AngleXU=0 Radius=1.5
  constraints (18):
    c: Coincident(g0,g1)
    c: Coincident(g1,g2)
    c: Coincident(g2,g3)
    c: Coincident(g3,g4)
    c: Coincident(g4,g5)
    c: Coincident(g5,g0)
    c: Equal(g0, g1-g5) x5
    c: PointOnObject(g0,g6)
    c: PointOnObject(g1,g6)
    c: PointOnObject(g2,g6)
    c: PointOnObject(g3,g6)
    c: PointOnObject(g4,g6)
    c: PointOnObject(g5,g6)
    c: Coincident(g6,g-1)
    c: PointOnObject(g5,g-2)
    c: DistanceX(g0,g4) = 5.5
    c: Coincident(g7,g-1)
    c: Radius(g7) = 1.5
FEATURE [PartDesign::Pad] Pad451  label="M3 Nut Primitive088"
  Length = 1.2
  Length2 = 1.2
  Profile = -> Sketch1036
  Type = 4
FEATURE [Sketcher::SketchObject] Sketch1037
  ExternalGeometry = -> [Pad451]
  MapMode = 5
  Placement = pos=(0,0,0) rot=(0.57735,0.57735,0.57735;2.0944rad)
  Support = -> [YZ_Plane360]
  sketch-geometry (6):
    g0: LineSegment StartX=-2.67543 StartY=1.2 StartZ=0 EndX=-3.67543 EndY=1.2 EndZ=0
    g1: LineSegment StartX=-3.67543 StartY=1.2 StartZ=0 EndX=-3.67543 EndY=-1.2 EndZ=0
    g2: LineSegment StartX=-3.67543 StartY=-1.2 StartZ=0 EndX=-2.67543 EndY=-1.2 EndZ=0
    g3: LineSegment StartX=-2.67543 StartY=-1.2 StartZ=0 EndX=-3.17543 EndY=-1 EndZ=0
    g4: LineSegment StartX=-3.17543 StartY=-1 StartZ=0 EndX=-3.17543 EndY=1 EndZ=0
    g5: LineSegment StartX=-3.17543 StartY=1 StartZ=0 EndX=-2.67543 EndY=1.2 EndZ=0
  constraints (15):
    c: Horizontal(g0)
    c: Coincident(g0,g1)
    c: Coincident(g1,g2)
    c: Coincident(g2,g3)
    c: Coincident(g3,g4)
    c: Coincident(g4,g5)
    c: Coincident(g5,g0)
    c: Symmetric(g4,g3,g-1)
    c: Symmetric(g0,g2,g-1)
    c: Symmetric(g1,g0,g-1)
    c: DistanceX(g0,g4) = 0.5
    c: DistanceY(g3,g4) = 2
    c: DistanceY(g1,g0) = 2.4
    c: PointOnObject(g3,g-3)
    c: DistanceX(g4,g0) = 0.5
FEATURE [PartDesign::Groove] Groove093  label="M3 Nut Smooth089"
  Angle = 360
  Axis = (-2e-16,3e-16,1)
  Base = (0,0,0)
  BaseFeature = -> Pad451
  Profile = -> Sketch1037
  ReferenceAxis = -> Sketch1037 [V_Axis]
  Reversed = true
FEATURE [PartDesign::Chamfer] Chamfer148  label="M3 Nut Smooth Hole061"
  Base = -> Groove093 [Edge24,Edge23]
  BaseFeature = -> Groove093
  Size = 0.2
FEATURE [PartDesign::Body] Body246  label="M3 Nut048"
  Group = -> [Sketch1036,Pad451,Sketch1037,Groove093,Chamfer148]
  Origin = -> Origin305
  Placement = pos=(5e-14,-55.6,224.85) rot=(0.57735,-0.57735,0.57735;4.18879rad)
  Tip = -> Chamfer148
FEATURE [Sketcher::SketchObject] Sketch1039
  MapMode = 5
  Placement = pos=(0,0,0) rot=(1,0,0;1.5708rad)
  Support = -> [XZ_Plane316]
  sketch-geometry (1):
    g0: Circle CenterX=1.55 CenterY=4 CenterZ=0 NormalX=0 NormalY=0 NormalZ=1 AngleXU=0 Radius=0.75
  constraints (3):
    c: Radius(g0) = 0.75
    c: DistanceY(g-1,g0) = 4
    c: DistanceX(g-1,g0) = 1.55
FEATURE [PartDesign::Pad] Pad458
  Length = 10
  Length2 = 100
  Placement = pos=(0,0,0) rot=(1,0,0;1.5708rad)
  Profile = -> Sketch1039
  Reversed = true
  Type = 0
FEATURE [PartDesign::Body] Body253  label="brown wire008"
  Group = -> [Sketch1039,Pad458]
  Origin = -> Origin303
  Placement = pos=(0,25.15,0) rot=(0,0,1;0rad)
  Tip = -> Pad458
FEATURE [Sketcher::SketchObject] Sketch1042
  ExternalGeometry = -> [Pad440]
  MapMode = 5
  Placement = pos=(0,0,37.6) rot=(0,0,1;0rad)
  Support = -> [Pad440]
  sketch-geometry (1):
    g0: Circle CenterX=-3e-16 CenterY=10.15 CenterZ=0 NormalX=0 NormalY=0 NormalZ=1 AngleXU=0 Radius=6.5
  constraints (2):
    c: Coincident(g0,g-3)
    c: Radius(g0) = 6.5
FEATURE [PartDesign::Pad] Pad460
  BaseFeature = -> Pad440
  Length = 1
  Length2 = 100
  Profile = -> Sketch1042
  Type = 0
FEATURE [Sketcher::SketchObject] Sketch1020
  ExternalGeometry = -> [Pad460]
  MapMode = 5
  Placement = pos=(0,0,38.6) rot=(0,0,1;0rad)
  Support = -> [Pad460]
  sketch-geometry (1):
    g0: Circle CenterX=0 CenterY=10.15 CenterZ=0 NormalX=0 NormalY=0 NormalZ=1 AngleXU=0 Radius=5.5
  constraints (2):
    c: Coincident(g0,g-3)
    c: Radius(g0) = 5.5
FEATURE [PartDesign::Pad] Pad455
  BaseFeature = -> Pad460
  Length = 0.5
  Length2 = 100
  Profile = -> Sketch1020
  Type = 0
FEATURE [Sketcher::SketchObject] Sketch1032
  ExternalGeometry = -> [Pad455]
  MapMode = 5
  Placement = pos=(0,0,39.1) rot=(0,0,1;0rad)
  Support = -> [Pad455]
  sketch-geometry (1):
    g0: Circle CenterX=0 CenterY=10.15 CenterZ=0 NormalX=0 NormalY=0 NormalZ=1 AngleXU=0 Radius=3
  constraints (2):
    c: Coincident(g0,g-3)
    c: Radius(g0) = 3
FEATURE [PartDesign::Pad] Pad466
  BaseFeature = -> Pad455
  Length = 4
  Length2 = 100
  Profile = -> Sketch1032
  Type = 0
FEATURE [Sketcher::SketchObject] Sketch1025
  ExternalGeometry = -> [Pad466]
  MapMode = 5
  Placement = pos=(0,0,43.1) rot=(0,0,1;0rad)
  Support = -> [Pad466]
  sketch-geometry (1):
    g0: Circle CenterX=0 CenterY=10.15 CenterZ=0 NormalX=0 NormalY=0 NormalZ=1 AngleXU=0 Radius=1.5
  constraints (2):
    c: Coincident(g0,g-3)
    c: Radius(g0) = 1.5
FEATURE [PartDesign::Pocket] Pocket417
  BaseFeature = -> Pad466
  Length = 5
  Length2 = 100
  Profile = -> Sketch1025
  Type = 0
FEATURE [Sketcher::SketchObject] Sketch1008
  MapMode = 5
  Placement = pos=(0,0,29.1) rot=(0,0,1;0rad)
  Support = -> [Pocket417]
  sketch-geometry (4):
    g0: Circle CenterX=-4.91157 CenterY=25.3 CenterZ=0 NormalX=0 NormalY=0 NormalZ=1 AngleXU=0 Radius=2.25
    g1: Circle CenterX=4.91157 CenterY=25.3 CenterZ=0 NormalX=0 NormalY=0 NormalZ=1 AngleXU=0 Radius=2.25
    g2: Circle CenterX=-4.91157 CenterY=-25.3 CenterZ=0 NormalX=0 NormalY=0 NormalZ=1 AngleXU=0 Radius=2.25
    g3: Circle CenterX=4.91157 CenterY=-25.3 CenterZ=0 NormalX=0 NormalY=0 NormalZ=1 AngleXU=0 Radius=2.25
  constraints (8):
    c: Equal(g3,g2)
    c: Equal(g2,g1)
    c: Equal(g1,g0)
    c: Radius(g1) = 2.25
    c: Symmetric(g1,g0,g-2)
    c: Symmetric(g3,g2,g-2)
    c: Symmetric(g3,g1,g-1)
    c: DistanceY(g3,g1) = 50.6
FEATURE [PartDesign::Pocket] Pocket416
  BaseFeature = -> Pocket417
  Length = 5
  Length2 = 100
  Profile = -> Sketch1008
  Type = 0
FEATURE [Sketcher::SketchObject] Sketch1041
  MapMode = 5
  Placement = pos=(0,0,29.1) rot=(0,0,1;0rad)
  Support = -> [Pocket416]
  sketch-geometry (8):
    g0: LineSegment StartX=-0.5 StartY=26.8 StartZ=0 EndX=0.5 EndY=26.8 EndZ=0
    g1: LineSegment StartX=0.5 StartY=26.8 StartZ=0 EndX=0.5 EndY=20.15 EndZ=0
    g2: LineSegment StartX=0.5 StartY=20.15 StartZ=0 EndX=-0.5 EndY=20.15 EndZ=0
    g3: LineSegment StartX=-0.5 StartY=20.15 StartZ=0 EndX=-0.5 EndY=26.8 EndZ=0
    g4: LineSegment StartX=-0.5 StartY=-20.15 StartZ=0 EndX=0.5 EndY=-20.15 EndZ=0
    g5: LineSegment StartX=0.5 StartY=-20.15 StartZ=0 EndX=0.5 EndY=-26.8 EndZ=0
    g6: LineSegment StartX=0.5 StartY=-26.8 StartZ=0 EndX=-0.5 EndY=-26.8 EndZ=0
    g7: LineSegment StartX=-0.5 StartY=-26.8 StartZ=0 EndX=-0.5 EndY=-20.15 EndZ=0
  constraints (20):
    c: Coincident(g0,g1)
    c: Coincident(g1,g2)
    c: Coincident(g2,g3)
    c: Coincident(g3,g0)
    c: Horizontal(g2)
    c: Vertical(g1)
    c: Vertical(g3)
    c: Coincident(g4,g5)
    c: Coincident(g5,g6)
    c: Coincident(g6,g7)
    c: Coincident(g7,g4)
    c: Horizontal(g6)
    c: Vertical(g7)
    c: Symmetric(g4,g4,g-2)
    c: Symmetric(g0,g0,g-2)
    c: Symmetric(g0,g5,g-1)
    c: DistanceY(g5,g0) = 53.6
    c: DistanceY(g4,g1) = 40.3
    c: DistanceX(g0,g0) = 1
    c: Symmetric(g4,g1,g-1)
FEATURE [PartDesign::Pad] Pad449
  BaseFeature = -> Pocket416
  Length = 2
  Length2 = 100
  Profile = -> Sketch1041
  Type = 0
FEATURE [Sketcher::SketchObject] Sketch1005
  ExternalGeometry = -> [Pad449]
  MapMode = 5
  Placement = pos=(0.5,0,0) rot=(0.57735,0.57735,0.57735;2.0944rad)
  Support = -> [Pad449]
  sketch-geometry (6):
    g0: LineSegment StartX=-26.8 StartY=29.1 StartZ=0 EndX=-26.8 EndY=31.1 EndZ=0
    g1: LineSegment StartX=-26.8 StartY=31.1 StartZ=0 EndX=-20.15 EndY=31.1 EndZ=0
    g2: LineSegment StartX=-20.15 StartY=31.1 StartZ=0 EndX=-26.8 EndY=29.1 EndZ=0
    g3: LineSegment StartX=20.15 StartY=31.1 StartZ=0 EndX=26.8 EndY=31.1 EndZ=0
    g4: LineSegment StartX=26.8 StartY=31.1 StartZ=0 EndX=26.8 EndY=29.1 EndZ=0
    g5: LineSegment StartX=26.8 StartY=29.1 StartZ=0 EndX=20.15 EndY=31.1 EndZ=0
  constraints (14):
    c: Vertical(g0)
    c: Coincident(g0,g1)
    c: Horizontal(g1)
    c: Coincident(g1,g2)
    c: Coincident(g2,g0)
    c: Coincident(g3,g4)
    c: Coincident(g4,g5)
    c: Coincident(g5,g3)
    c: Symmetric(g0,g4,g-2)
    c: Symmetric(g3,g0,g-2)
    c: Symmetric(g1,g3,g-2)
    c: DistanceX(g0,g3) = 53.6
    c: DistanceY(g4,g4) = 2
    c: Coincident(g3,g-3)
FEATURE [PartDesign::Pocket] Pocket415
  BaseFeature = -> Pad449
  Length = 1
  Length2 = 100
  Profile = -> Sketch1005
  Type = 0
FEATURE [PartDesign::Fillet] Fillet090
  Base = -> Pocket415 [Edge26,Edge27,Edge72,Edge63,Edge70,Edge78,Edge51,Edge49,Edge71,Edge50,Edge79,Edge86,Edge30,Edge21,Edge4,Edge29,Edge105,Edge107,Edge109,Edge111,Edge113,Edge114,Edge123]
  BaseFeature = -> Pocket415
  Radius = 0.4
FEATURE [Sketcher::SketchObject] Sketch1031
  MapMode = 5
  Placement = pos=(0,20.15,0) rot=(0,0.707107,0.707107;3.14159rad)
  Support = -> [Fillet090]
  sketch-geometry (4):
    g0: LineSegment StartX=-3.25 StartY=2 StartZ=0 EndX=3.25 EndY=2 EndZ=0
    g1: LineSegment StartX=3.25 StartY=2 StartZ=0 EndX=3.25 EndY=6 EndZ=0
    g2: LineSegment StartX=3.25 StartY=6 StartZ=0 EndX=-3.25 EndY=6 EndZ=0
    g3: LineSegment StartX=-3.25 StartY=6 StartZ=0 EndX=-3.25 EndY=2 EndZ=0
  constraints (11):
    c: Coincident(g0,g1)
    c: Coincident(g1,g2)
    c: Coincident(g2,g3)
    c: Coincident(g3,g0)
    c: Horizontal(g0)
    c: Vertical(g1)
    c: Vertical(g3)
    c: DistanceY(g-1,g0) = 2
    c: DistanceY(g1,g1) = 4
    c: Symmetric(g2,g1,g-2)
    c: DistanceX(g2,g2) = 6.5
FEATURE [PartDesign::Pad] Pad469
  BaseFeature = -> Fillet090
  Length = 1
  Length2 = 100
  Profile = -> Sketch1031
  Type = 0
FEATURE [Sketcher::SketchObject] Sketch1019
  MapMode = 5
  Placement = pos=(0,21.15,0) rot=(0,0.707107,0.707107;3.14159rad)
  Support = -> [Pad469]
  sketch-geometry (4):
    g0: LineSegment StartX=-2.75 StartY=5.5 StartZ=0 EndX=2.75 EndY=5.5 EndZ=0
    g1: LineSegment StartX=2.75 StartY=5.5 StartZ=0 EndX=2.75 EndY=2.5 EndZ=0
    g2: LineSegment StartX=2.75 StartY=2.5 StartZ=0 EndX=-2.75 EndY=2.5 EndZ=0
    g3: LineSegment StartX=-2.75 StartY=2.5 StartZ=0 EndX=-2.75 EndY=5.5 EndZ=0
  constraints (11):
    c: Coincident(g0,g1)
    c: Coincident(g1,g2)
    c: Coincident(g2,g3)
    c: Coincident(g3,g0)
    c: Horizontal(g0)
    c: Vertical(g1)
    c: Vertical(g3)
    c: Symmetric(g1,g2,g-2)
    c: DistanceY(g1,g0) = 3
    c: DistanceY(g-1,g1) = 2.5
    c: DistanceX(g0,g0) = 5.5
FEATURE [PartDesign::Pad] Pad448
  BaseFeature = -> Pad469
  Length = 4
  Length2 = 100
  Profile = -> Sketch1019
  Type = 0
FEATURE [Sketcher::SketchObject] Sketch1043
  MapMode = 5
  Placement = pos=(0,0,0) rot=(1,0,0;3.14159rad)
  Support = -> [Pad448]
  sketch-geometry (4):
    g0: LineSegment StartX=-10 StartY=-20.15 StartZ=0 EndX=10 EndY=-20.15 EndZ=0
    g1: LineSegment StartX=10 StartY=-20.15 StartZ=0 EndX=10 EndY=20.15 EndZ=0
    g2: LineSegment StartX=10 StartY=20.15 StartZ=0 EndX=-10 EndY=20.15 EndZ=0
    g3: LineSegment StartX=-10 StartY=20.15 StartZ=0 EndX=-10 EndY=-20.15 EndZ=0
  constraints (10):
    c: Coincident(g0,g1)
    c: Coincident(g1,g2)
    c: Coincident(g2,g3)
    c: Coincident(g3,g0)
    c: Horizontal(g0)
    c: Vertical(g1)
    c: Symmetric(g2,g1,g-2)
    c: Symmetric(g0,g2,g-1)
    c: DistanceX(g2,g2) = 20
    c: DistanceY(g1,g1) = 40.3
FEATURE [PartDesign::Pad] Pad470
  BaseFeature = -> Pad448
  Length = 2
  Length2 = 100
  Profile = -> Sketch1043
  Type = 0
FEATURE [PartDesign::Chamfer] Chamfer154
  Base = -> Pad470 [Face7]
  BaseFeature = -> Pad470
  Size = 1.5
FEATURE [PartDesign::Fillet] Fillet091
  Base = -> Chamfer154 [Edge1,Edge7,Edge18,Edge4,Face12]
  BaseFeature = -> Chamfer154
  Radius = 0.4
FEATURE [Sketcher::SketchObject] Sketch1023
  ExternalGeometry = -> [Fillet091]
  MapMode = 5
  Placement = pos=(0,0,43.1) rot=(0,0,1;0rad)
  Support = -> [Fillet091]
  sketch-geometry (1):
    g0: Circle CenterX=0 CenterY=10.15 CenterZ=0 NormalX=0 NormalY=0 NormalZ=1 AngleXU=0 Radius=3
  constraints (2):
    c: Coincident(g0,g-3)
    c: Radius(g0) = 3
FEATURE [PartDesign::Pocket] Pocket421
  BaseFeature = -> Fillet091
  Length = 5
  Length2 = 100
  Profile = -> Sketch1023
  Type = 0
FEATURE [PartDesign::Body] Body258  label="MG996R007"
  Group = -> [Sketch1033,Pad464,Sketch1029,Pad463,Sketch1017,Pad454,Sketch1030,Pad440,Sketch1042,Pad460,Sketch1020,Pad455,Sketch1032,Pad466,Sketch1025,Pocket417,Sketch1008,Pocket416,Sketch1041,Pad449,Sketch1005,Pocket415,Fillet090,Sketch1031,Pad469,Sketch1019,Pad448,Sketch1043,Pad470,Chamfer154,Fillet091,Sketch1023,Pocket421]
  Origin = -> Origin277
  Tip = -> Pocket421
FEATURE [Sketcher::SketchObject] Sketch1044
  MapMode = 5
  Placement = pos=(0,0,0) rot=(1,0,0;1.5708rad)
  Support = -> [XZ_Plane313]
  sketch-geometry (1):
    g0: Circle CenterX=-1.55 CenterY=4 CenterZ=0 NormalX=0 NormalY=0 NormalZ=1 AngleXU=0 Radius=0.75
  constraints (3):
    c: Radius(g0) = 0.75
    c: DistanceY(g-1,g0) = 4
    c: DistanceX(g0,g-1) = 1.55
FEATURE [PartDesign::Pad] Pad438
  Length = 10
  Length2 = 100
  Placement = pos=(0,0,0) rot=(1,0,0;1.5708rad)
  Profile = -> Sketch1044
  Reversed = true
  Type = 0
FEATURE [PartDesign::Body] Body248  label="orange wire008"
  Group = -> [Sketch1044,Pad438]
  Origin = -> Origin312
  Placement = pos=(0,25.15,0) rot=(0,0,1;0rad)
  Tip = -> Pad438
FEATURE [Sketcher::SketchObject] Sketch1045
  MapMode = 5
  Support = -> [XY_Plane364]
  sketch-geometry (1):
    g0: Circle CenterX=0 CenterY=0 CenterZ=0 NormalX=0 NormalY=0 NormalZ=1 AngleXU=0 Radius=2.75
  constraints (2):
    c: Coincident(g0,g-1)
    c: Radius(g0) = 2.75
FEATURE [PartDesign::Pad] Pad465  label="M3x20 Head037"
  Length = 3
  Length2 = 100
  Profile = -> Sketch1045
  Type = 0
FEATURE [Sketcher::SketchObject] Sketch1046
  MapMode = 5
  Support = -> [XY_Plane318]
  sketch-geometry (1):
    g0: Circle CenterX=0 CenterY=10.15 CenterZ=0 NormalX=0 NormalY=0 NormalZ=1 AngleXU=0 Radius=3
  constraints (3):
    c: PointOnObject(g0,g-2)
    c: DistanceY(g-1,g0) = 10.15
    c: Radius(g0) = 3
FEATURE [PartDesign::Pad] Pad450
  Length = 5
  Length2 = 100
  Profile = -> Sketch1046
  Type = 0
FEATURE [Sketcher::SketchObject] Sketch1021
  ExternalGeometry = -> [Pad450]
  MapMode = 5
  Placement = pos=(0,0,5) rot=(0,0,1;0rad)
  Support = -> [Pad450]
  sketch-geometry (1):
    g0: Circle CenterX=0 CenterY=10.15 CenterZ=0 NormalX=0 NormalY=0 NormalZ=1 AngleXU=0 Radius=1.5
  constraints (2):
    c: Coincident(g0,g-3)
    c: Radius(g0) = 1.5
FEATURE [PartDesign::Pocket] Pocket418
  BaseFeature = -> Pad450
  Length = 4
  Length2 = 100
  Profile = -> Sketch1021
  Type = 0
FEATURE [PartDesign::Chamfer] Chamfer143
  Base = -> Pocket418 [Edge3]
  BaseFeature = -> Pocket418
  Size = 0.25
FEATURE [PartDesign::Body] Body259  label="Gear008"
  Group = -> [Sketch1046,Pad450,Sketch1021,Pocket418,Chamfer143]
  Origin = -> Origin286
  Placement = pos=(0,0,38.25) rot=(0,0,1;0rad)
  Tip = -> Chamfer143
FEATURE [App::Part] Part098  label="Servo005"
  Group = -> [Body258,Body259,Body271,Body248,Body253]
  Origin = -> Origin313
  Placement = pos=(-21.1341,-60.6,200.491) rot=(0.57735,0.57735,0.57735;2.0944rad)
FEATURE [Sketcher::SketchObject] Sketch1047
  MapMode = 5
  Support = -> [XY_Plane368]
  sketch-geometry (8):
    g0: LineSegment StartX=0 StartY=3.17543 StartZ=0 EndX=-2.75 EndY=1.58771 EndZ=0
    g1: LineSegment StartX=-2.75 StartY=1.58771 StartZ=0 EndX=-2.75 EndY=-1.58771 EndZ=0
    g2: LineSegment StartX=-2.75 StartY=-1.58771 StartZ=0 EndX=0 EndY=-3.17543 EndZ=0
    g3: LineSegment StartX=0 StartY=-3.17543 StartZ=0 EndX=2.75 EndY=-1.58771 EndZ=0
    g4: LineSegment StartX=2.75 StartY=-1.58771 StartZ=0 EndX=2.75 EndY=1.58771 EndZ=0
    g5: LineSegment StartX=2.75 StartY=1.58771 StartZ=0 EndX=0 EndY=3.17543 EndZ=0
    g6: Circle [constr] CenterX=0 CenterY=0 CenterZ=0 NormalX=0 NormalY=0 NormalZ=1 AngleXU=0 Radius=3.17543
    g7: Circle CenterX=0 CenterY=0 CenterZ=0 NormalX=0 NormalY=0 NormalZ=1 AngleXU=0 Radius=1.5
  constraints (18):
    c: Coincident(g0,g1)
    c: Coincident(g1,g2)
    c: Coincident(g2,g3)
    c: Coincident(g3,g4)
    c: Coincident(g4,g5)
    c: Coincident(g5,g0)
    c: Equal(g0, g1-g5) x5
    c: PointOnObject(g0,g6)
    c: PointOnObject(g1,g6)
    c: PointOnObject(g2,g6)
    c: PointOnObject(g3,g6)
    c: PointOnObject(g4,g6)
    c: PointOnObject(g5,g6)
    c: Coincident(g6,g-1)
    c: PointOnObject(g5,g-2)
    c: DistanceX(g0,g4) = 5.5
    c: Coincident(g7,g-1)
    c: Radius(g7) = 1.5
FEATURE [PartDesign::Pad] Pad456  label="M3 Nut Primitive090"
  Length = 1.2
  Length2 = 1.2
  Profile = -> Sketch1047
  Type = 4
FEATURE [Sketcher::SketchObject] Sketch1038
  ExternalGeometry = -> [Pad456]
  MapMode = 5
  Placement = pos=(0,0,0) rot=(0.57735,0.57735,0.57735;2.0944rad)
  Support = -> [YZ_Plane353]
  sketch-geometry (6):
    g0: LineSegment StartX=-2.67543 StartY=1.2 StartZ=0 EndX=-3.67543 EndY=1.2 EndZ=0
    g1: LineSegment StartX=-3.67543 StartY=1.2 StartZ=0 EndX=-3.67543 EndY=-1.2 EndZ=0
    g2: LineSegment StartX=-3.67543 StartY=-1.2 StartZ=0 EndX=-2.67543 EndY=-1.2 EndZ=0
    g3: LineSegment StartX=-2.67543 StartY=-1.2 StartZ=0 EndX=-3.17543 EndY=-1 EndZ=0
    g4: LineSegment StartX=-3.17543 StartY=-1 StartZ=0 EndX=-3.17543 EndY=1 EndZ=0
    g5: LineSegment StartX=-3.17543 StartY=1 StartZ=0 EndX=-2.67543 EndY=1.2 EndZ=0
  constraints (15):
    c: Horizontal(g0)
    c: Coincident(g0,g1)
    c: Coincident(g1,g2)
    c: Coincident(g2,g3)
    c: Coincident(g3,g4)
    c: Coincident(g4,g5)
    c: Coincident(g5,g0)
    c: Symmetric(g4,g3,g-1)
    c: Symmetric(g0,g2,g-1)
    c: Symmetric(g1,g0,g-1)
    c: DistanceX(g0,g4) = 0.5
    c: DistanceY(g3,g4) = 2
    c: DistanceY(g1,g0) = 2.4
    c: PointOnObject(g3,g-3)
    c: DistanceX(g4,g0) = 0.5
FEATURE [PartDesign::Groove] Groove095  label="M3 Nut Smooth091"
  Angle = 360
  Axis = (-2e-16,3e-16,1)
  Base = (0,0,0)
  BaseFeature = -> Pad456
  Profile = -> Sketch1038
  ReferenceAxis = -> Sketch1038 [V_Axis]
  Reversed = true
FEATURE [PartDesign::Chamfer] Chamfer139  label="M3 Nut Smooth Hole059"
  Base = -> Groove095 [Edge24,Edge23]
  BaseFeature = -> Groove095
  Size = 0.2
FEATURE [PartDesign::Body] Body247  label="M3 Nut049"
  Group = -> [Sketch1047,Pad456,Sketch1038,Groove095,Chamfer139]
  Origin = -> Origin291
  Placement = pos=(3.9e-14,-65.6,176.35) rot=(0.57735,-0.57735,0.57735;4.18879rad)
  Tip = -> Chamfer139
FEATURE [Sketcher::SketchObject] Sketch1049
  MapMode = 5
  Support = -> [XY_Plane355]
  sketch-geometry (8):
    g0: LineSegment StartX=0 StartY=3.17543 StartZ=0 EndX=-2.75 EndY=1.58771 EndZ=0
    g1: LineSegment StartX=-2.75 StartY=1.58771 StartZ=0 EndX=-2.75 EndY=-1.58771 EndZ=0
    g2: LineSegment StartX=-2.75 StartY=-1.58771 StartZ=0 EndX=0 EndY=-3.17543 EndZ=0
    g3: LineSegment StartX=0 StartY=-3.17543 StartZ=0 EndX=2.75 EndY=-1.58771 EndZ=0
    g4: LineSegment StartX=2.75 StartY=-1.58771 StartZ=0 EndX=2.75 EndY=1.58771 EndZ=0
    g5: LineSegment StartX=2.75 StartY=1.58771 StartZ=0 EndX=0 EndY=3.17543 EndZ=0
    g6: Circle [constr] CenterX=0 CenterY=0 CenterZ=0 NormalX=0 NormalY=0 NormalZ=1 AngleXU=0 Radius=3.17543
    g7: Circle CenterX=0 CenterY=0 CenterZ=0 NormalX=0 NormalY=0 NormalZ=1 AngleXU=0 Radius=1.5
  constraints (18):
    c: Coincident(g0,g1)
    c: Coincident(g1,g2)
    c: Coincident(g2,g3)
    c: Coincident(g3,g4)
    c: Coincident(g4,g5)
    c: Coincident(g5,g0)
    c: Equal(g0, g1-g5) x5
    c: PointOnObject(g0,g6)
    c: PointOnObject(g1,g6)
    c: PointOnObject(g2,g6)
    c: PointOnObject(g3,g6)
    c: PointOnObject(g4,g6)
    c: PointOnObject(g5,g6)
    c: Coincident(g6,g-1)
    c: PointOnObject(g5,g-2)
    c: DistanceX(g0,g4) = 5.5
    c: Coincident(g7,g-1)
    c: Radius(g7) = 1.5
FEATURE [PartDesign::Pad] Pad453  label="M3 Nut Primitive089"
  Length = 1.2
  Length2 = 1.2
  Profile = -> Sketch1049
  Type = 4
FEATURE [Sketcher::SketchObject] Sketch1040
  ExternalGeometry = -> [Pad453]
  MapMode = 5
  Placement = pos=(0,0,0) rot=(0.57735,0.57735,0.57735;2.0944rad)
  Support = -> [YZ_Plane362]
  sketch-geometry (6):
    g0: LineSegment StartX=-2.67543 StartY=1.2 StartZ=0 EndX=-3.67543 EndY=1.2 EndZ=0
    g1: LineSegment StartX=-3.67543 StartY=1.2 StartZ=0 EndX=-3.67543 EndY=-1.2 EndZ=0
    g2: LineSegment StartX=-3.67543 StartY=-1.2 StartZ=0 EndX=-2.67543 EndY=-1.2 EndZ=0
    g3: LineSegment StartX=-2.67543 StartY=-1.2 StartZ=0 EndX=-3.17543 EndY=-1 EndZ=0
    g4: LineSegment StartX=-3.17543 StartY=-1 StartZ=0 EndX=-3.17543 EndY=1 EndZ=0
    g5: LineSegment StartX=-3.17543 StartY=1 StartZ=0 EndX=-2.67543 EndY=1.2 EndZ=0
  constraints (15):
    c: Horizontal(g0)
    c: Coincident(g0,g1)
    c: Coincident(g1,g2)
    c: Coincident(g2,g3)
    c: Coincident(g3,g4)
    c: Coincident(g4,g5)
    c: Coincident(g5,g0)
    c: Symmetric(g4,g3,g-1)
    c: Symmetric(g0,g2,g-1)
    c: Symmetric(g1,g0,g-1)
    c: DistanceX(g0,g4) = 0.5
    c: DistanceY(g3,g4) = 2
    c: DistanceY(g1,g0) = 2.4
    c: PointOnObject(g3,g-3)
    c: DistanceX(g4,g0) = 0.5
FEATURE [PartDesign::Groove] Groove094  label="M3 Nut Smooth090"
  Angle = 360
  Axis = (-2e-16,3e-16,1)
  Base = (0,0,0)
  BaseFeature = -> Pad453
  Profile = -> Sketch1040
  ReferenceAxis = -> Sketch1040 [V_Axis]
  Reversed = true
FEATURE [PartDesign::Chamfer] Chamfer137  label="M3 Nut Smooth Hole058"
  Base = -> Groove094 [Edge24,Edge23]
  BaseFeature = -> Groove094
  Size = 0.2
FEATURE [PartDesign::Body] Body252  label="M3 Nut050"
  Group = -> [Sketch1049,Pad453,Sketch1040,Groove094,Chamfer137]
  Origin = -> Origin265
  Placement = pos=(1.5e-14,-55.6,176.35) rot=(0.57735,-0.57735,0.57735;4.18879rad)
  Tip = -> Chamfer137
FEATURE [Sketcher::SketchObject] Sketch1053
  MapMode = 5
  Support = -> [XY_Plane367]
  sketch-geometry (8):
    g0: LineSegment StartX=0 StartY=3.17543 StartZ=0 EndX=-2.75 EndY=1.58771 EndZ=0
    g1: LineSegment StartX=-2.75 StartY=1.58771 StartZ=0 EndX=-2.75 EndY=-1.58771 EndZ=0
    g2: LineSegment StartX=-2.75 StartY=-1.58771 StartZ=0 EndX=0 EndY=-3.17543 EndZ=0
    g3: LineSegment StartX=0 StartY=-3.17543 StartZ=0 EndX=2.75 EndY=-1.58771 EndZ=0
    g4: LineSegment StartX=2.75 StartY=-1.58771 StartZ=0 EndX=2.75 EndY=1.58771 EndZ=0
    g5: LineSegment StartX=2.75 StartY=1.58771 StartZ=0 EndX=0 EndY=3.17543 EndZ=0
    g6: Circle [constr] CenterX=0 CenterY=0 CenterZ=0 NormalX=0 NormalY=0 NormalZ=1 AngleXU=0 Radius=3.17543
    g7: Circle CenterX=0 CenterY=0 CenterZ=0 NormalX=0 NormalY=0 NormalZ=1 AngleXU=0 Radius=1.5
  constraints (18):
    c: Coincident(g0,g1)
    c: Coincident(g1,g2)
    c: Coincident(g2,g3)
    c: Coincident(g3,g4)
    c: Coincident(g4,g5)
    c: Coincident(g5,g0)
    c: Equal(g0, g1-g5) x5
    c: PointOnObject(g0,g6)
    c: PointOnObject(g1,g6)
    c: PointOnObject(g2,g6)
    c: PointOnObject(g3,g6)
    c: PointOnObject(g4,g6)
    c: PointOnObject(g5,g6)
    c: Coincident(g6,g-1)
    c: PointOnObject(g5,g-2)
    c: DistanceX(g0,g4) = 5.5
    c: Coincident(g7,g-1)
    c: Radius(g7) = 1.5
FEATURE [PartDesign::Pad] Pad461  label="M3 Nut Primitive091"
  Length = 1.2
  Length2 = 1.2
  Profile = -> Sketch1053
  Type = 4
FEATURE [Sketcher::SketchObject] Sketch1050
  ExternalGeometry = -> [Pad461]
  MapMode = 5
  Placement = pos=(0,0,0) rot=(0.57735,0.57735,0.57735;2.0944rad)
  Support = -> [YZ_Plane354]
  sketch-geometry (6):
    g0: LineSegment StartX=-2.67543 StartY=1.2 StartZ=0 EndX=-3.67543 EndY=1.2 EndZ=0
    g1: LineSegment StartX=-3.67543 StartY=1.2 StartZ=0 EndX=-3.67543 EndY=-1.2 EndZ=0
    g2: LineSegment StartX=-3.67543 StartY=-1.2 StartZ=0 EndX=-2.67543 EndY=-1.2 EndZ=0
    g3: LineSegment StartX=-2.67543 StartY=-1.2 StartZ=0 EndX=-3.17543 EndY=-1 EndZ=0
    g4: LineSegment StartX=-3.17543 StartY=-1 StartZ=0 EndX=-3.17543 EndY=1 EndZ=0
    g5: LineSegment StartX=-3.17543 StartY=1 StartZ=0 EndX=-2.67543 EndY=1.2 EndZ=0
  constraints (15):
    c: Horizontal(g0)
    c: Coincident(g0,g1)
    c: Coincident(g1,g2)
    c: Coincident(g2,g3)
    c: Coincident(g3,g4)
    c: Coincident(g4,g5)
    c: Coincident(g5,g0)
    c: Symmetric(g4,g3,g-1)
    c: Symmetric(g0,g2,g-1)
    c: Symmetric(g1,g0,g-1)
    c: DistanceX(g0,g4) = 0.5
    c: DistanceY(g3,g4) = 2
    c: DistanceY(g1,g0) = 2.4
    c: PointOnObject(g3,g-3)
    c: DistanceX(g4,g0) = 0.5
FEATURE [PartDesign::Groove] Groove092  label="M3 Nut Smooth088"
  Angle = 360
  Axis = (-2e-16,3e-16,1)
  Base = (0,0,0)
  BaseFeature = -> Pad461
  Profile = -> Sketch1050
  ReferenceAxis = -> Sketch1050 [V_Axis]
  Reversed = true
FEATURE [PartDesign::Chamfer] Chamfer140  label="M3 Nut Smooth Hole060"
  Base = -> Groove092 [Edge24,Edge23]
  BaseFeature = -> Groove092
  Size = 0.2
FEATURE [PartDesign::Body] Body255  label="M3 Nut051"
  Group = -> [Sketch1053,Pad461,Sketch1050,Groove092,Chamfer140]
  Origin = -> Origin307
  Placement = pos=(5e-14,-65.6,224.85) rot=(0.57735,-0.57735,0.57735;4.18879rad)
  Tip = -> Chamfer140
FEATURE [Sketcher::SketchObject] Sketch1054
  MapMode = 5
  Support = -> [XY_Plane356]
  sketch-geometry (1):
    g0: Circle CenterX=0 CenterY=0 CenterZ=0 NormalX=0 NormalY=0 NormalZ=1 AngleXU=0 Radius=2.75
  constraints (2):
    c: Coincident(g0,g-1)
    c: Radius(g0) = 2.75
FEATURE [PartDesign::Pad] Pad459  label="M3x20 Head036"
  Length = 3
  Length2 = 100
  Profile = -> Sketch1054
  Type = 0
FEATURE [Sketcher::SketchObject] Sketch1051
  MapMode = 5
  Placement = pos=(0,0,3) rot=(0,0,1;0rad)
  Support = -> [Pad459]
  sketch-geometry (1):
    g0: Circle CenterX=0 CenterY=0 CenterZ=0 NormalX=0 NormalY=0 NormalZ=1 AngleXU=0 Radius=1.5
  constraints (2):
    c: Coincident(g0,g-1)
    c: Radius(g0) = 1.5
FEATURE [PartDesign::Pad] Pad452  label="M3x20 Thread036"
  BaseFeature = -> Pad459
  Length = 20
  Length2 = 100
  Profile = -> Sketch1051
  Type = 0
FEATURE [Sketcher::SketchObject] Sketch1048
  MapMode = 5
  Placement = pos=(0,0,0) rot=(1,0,0;3.14159rad)
  Support = -> [Pad452]
  sketch-geometry (7):
    g0: LineSegment StartX=1.275 StartY=0.736122 StartZ=0 EndX=0 EndY=1.47224 EndZ=0
    g1: LineSegment StartX=0 StartY=1.47224 StartZ=0 EndX=-1.275 EndY=0.736122 EndZ=0
    g2: LineSegment StartX=-1.275 StartY=0.736122 StartZ=0 EndX=-1.275 EndY=-0.736122 EndZ=0
    g3: LineSegment StartX=-1.275 StartY=-0.736122 StartZ=0 EndX=1.34766e-11 EndY=-1.47224 EndZ=0
    g4: LineSegment StartX=1.34766e-11 StartY=-1.47224 StartZ=0 EndX=1.275 EndY=-0.736122 EndZ=0
    g5: LineSegment StartX=1.275 StartY=-0.736122 StartZ=0 EndX=1.275 EndY=0.736122 EndZ=0
    g6: Circle [constr] CenterX=0 CenterY=0 CenterZ=0 NormalX=0 NormalY=0 NormalZ=1 AngleXU=0 Radius=1.47224
  constraints (16):
    c: Coincident(g0,g1)
    c: Coincident(g1,g2)
    c: Coincident(g2,g3)
    c: Coincident(g3,g4)
    c: Coincident(g4,g5)
    c: Coincident(g5,g0)
    c: Equal(g0, g1-g5) x5
    c: PointOnObject(g0,g6)
    c: PointOnObject(g1,g6)
    c: PointOnObject(g2,g6)
    c: PointOnObject(g3,g6)
    c: PointOnObject(g4,g6)
    c: PointOnObject(g5,g6)
    c: Coincident(g6,g-1)
    c: PointOnObject(g0,g-2)
    c: DistanceX(g1,g0) = 2.55
FEATURE [PartDesign::Pocket] Pocket422  label="M3x20 Wrench038"
  BaseFeature = -> Pad452
  Length = 1.3
  Length2 = 100
  Profile = -> Sketch1048
  Type = 0
FEATURE [PartDesign::Chamfer] Chamfer147  label="M3x20 Smooth028"
  Base = -> Pocket422 [Face11,Edge2,Edge24,Edge3]
  BaseFeature = -> Pocket422
  Size = 0.2
FEATURE [PartDesign::Body] Body257  label="M3x061"
  Group = -> [Sketch1054,Pad459,Sketch1051,Pad452,Sketch1048,Pocket422,Chamfer147]
  Origin = -> Origin284
  Placement = pos=(11.25,-65.6,224.85) rot=(0,-1,0;1.5708rad)
  Tip = -> Chamfer147
FEATURE [Sketcher::SketchObject] Sketch1055
  MapMode = 5
  Placement = pos=(0,0,2) rot=(0,0,1;0rad)
  Support = -> [Pad407]
  sketch-geometry (1):
    g0: Circle CenterX=0 CenterY=0 CenterZ=0 NormalX=0 NormalY=0 NormalZ=1 AngleXU=0 Radius=1
  constraints (2):
    c: Coincident(g0,g-1)
    c: Radius(g0) = 1
FEATURE [PartDesign::Pad] Pad424  label="M3x8 Thread049"
  BaseFeature = -> Pad407
  Length = 8
  Length2 = 100
  Profile = -> Sketch1055
  Type = 0
FEATURE [Sketcher::SketchObject] Sketch982
  MapMode = 5
  Placement = pos=(0,0,0) rot=(1,0,0;3.14159rad)
  Support = -> [Pad424]
  sketch-geometry (7):
    g0: LineSegment StartX=0.77 StartY=0.44456 StartZ=0 EndX=0 EndY=0.889119 EndZ=0
    g1: LineSegment StartX=0 StartY=0.889119 StartZ=0 EndX=-0.77 EndY=0.44456 EndZ=0
    g2: LineSegment StartX=-0.77 StartY=0.44456 StartZ=0 EndX=-0.77 EndY=-0.44456 EndZ=0
    g3: LineSegment StartX=-0.77 StartY=-0.44456 StartZ=0 EndX=3.85628e-11 EndY=-0.889119 EndZ=0
    g4: LineSegment StartX=3.85628e-11 StartY=-0.889119 StartZ=0 EndX=0.77 EndY=-0.44456 EndZ=0
    g5: LineSegment StartX=0.77 StartY=-0.44456 StartZ=0 EndX=0.77 EndY=0.44456 EndZ=0
    g6: Circle [constr] CenterX=0 CenterY=0 CenterZ=0 NormalX=0 NormalY=0 NormalZ=1 AngleXU=0 Radius=0.889119
  constraints (16):
    c: Coincident(g0,g1)
    c: Coincident(g1,g2)
    c: Coincident(g2,g3)
    c: Coincident(g3,g4)
    c: Coincident(g4,g5)
    c: Coincident(g5,g0)
    c: Equal(g0, g1-g5) x5
    c: PointOnObject(g0,g6)
    c: PointOnObject(g1,g6)
    c: PointOnObject(g2,g6)
    c: PointOnObject(g3,g6)
    c: PointOnObject(g4,g6)
    c: PointOnObject(g5,g6)
    c: Coincident(g6,g-1)
    c: PointOnObject(g0,g-2)
    c: DistanceX(g1,g0) = 1.54
FEATURE [PartDesign::Pocket] Pocket390  label="M3x8 Wrench046"
  BaseFeature = -> Pad424
  Length = 1
  Length2 = 100
  Profile = -> Sketch982
  Type = 0
FEATURE [PartDesign::Chamfer] Chamfer138  label="M3x8 Smooth038"
  Base = -> Pocket390 [Face11,Edge2,Edge24,Edge3]
  BaseFeature = -> Pocket390
  Size = 0.2
FEATURE [PartDesign::Body] Body241  label="M2x043"
  Group = -> [Sketch988,Pad407,Sketch1055,Pad424,Sketch982,Pocket390,Chamfer138]
  Origin = -> Origin281
  Tip = -> Chamfer138
FEATURE [App::Part] Part077  label="M029"
  Group = -> [Body241,Body207]
  Origin = -> Origin272
  Placement = pos=(-9.8e-15,10.5,80) rot=(0,1,0;3.14159rad)
FEATURE [Sketcher::SketchObject] Sketch1056
  MapMode = 5
  Placement = pos=(0,0,0) rot=(1,0,0;3.14159rad)
  Support = -> [Pocket385]
  sketch-geometry (2):
    g0: Circle CenterX=0 CenterY=0 CenterZ=0 NormalX=0 NormalY=0 NormalZ=1 AngleXU=0 Radius=4.5
    g1: Circle CenterX=0 CenterY=0 CenterZ=0 NormalX=0 NormalY=0 NormalZ=1 AngleXU=0 Radius=3
  constraints (4):
    c: Coincident(g0,g-1)
    c: Coincident(g1,g0)
    c: Radius(g0) = 4.5
    c: Radius(g1) = 3
FEATURE [PartDesign::Pad] Pad418
  BaseFeature = -> Pocket385
  Length = 3
  Length2 = 100
  Profile = -> Sketch1056
  Type = 0
FEATURE [PartDesign::Fillet] Fillet092
  Base = -> Pad418 [Face5,Edge96,Face4]
  BaseFeature = -> Pad418
  Radius = 0.2
FEATURE [Sketcher::SketchObject] Sketch1007
  ExternalGeometry = -> [Fillet092]
  MapMode = 5
  Support = -> [XY_Plane333]
  sketch-geometry (3):
    g0: ArcOfCircle [constr] CenterX=-2e-16 CenterY=-3e-16 CenterZ=0 NormalX=0 NormalY=0 NormalZ=1 AngleXU=0 Radius=13.5 StartAngle=3.66519 EndAngle=5.75959
    g1: ArcOfCircle [constr] CenterX=-2e-16 CenterY=-3e-16 CenterZ=0 NormalX=0 NormalY=0 NormalZ=1 AngleXU=0 Radius=13.5 StartAngle=2.61799 EndAngle=3.66519
    g2: LineSegment StartX=-11.6913 StartY=-6.75 StartZ=0 EndX=11.6913 EndY=6.75 EndZ=0
  constraints (9):
    c: Coincident(g0,g-5)
    c: Coincident(g0,g-4)
    c: Coincident(g1,g0)
    c: Coincident(g1,g0)
    c: Angle(g0) = 2.0944
    c: Angle(g1) = 1.0472
    c: Coincident(g1,g-3)
    c: Coincident(g2,g0)
    c: Coincident(g2,g-6)
FEATURE [PartDesign::Body] Body251  label="Futuba FSH6B005"
  Group = -> [Sketch983,Pad403,Sketch957,Pocket389,Sketch972,Pocket388,Sketch968,Pocket385,Sketch1056,Pad418,Fillet092,Sketch1007]
  Origin = -> Origin263
  Tip = -> Fillet092
FEATURE [App::Part] Part070  label="Servphorn001"
  Group = -> [Body251]
  Origin = -> Origin289
  Placement = pos=(0,0,3.45) rot=(0,0,1;0rad)
FEATURE [Sketcher::SketchObject] Sketch1057
  MapMode = 5
  Support = -> [XY_Plane349]
FEATURE [Sketcher::SketchObject] Sketch1059
  MapMode = 5
  Support = -> [XY_Plane313]
  sketch-geometry (1):
    g0: Circle CenterX=0 CenterY=0 CenterZ=0 NormalX=0 NormalY=0 NormalZ=1 AngleXU=0 Radius=1.9
  constraints (2):
    c: Coincident(g0,g-1)
    c: Radius(g0) = 1.9
FEATURE [PartDesign::Pad] Pad415  label="M3x8 Head050"
  Length = 2
  Length2 = 100
  Profile = -> Sketch1059
  Type = 0
FEATURE [Sketcher::SketchObject] Sketch1061
  MapMode = 5
  Support = -> [XY_Plane311]
  sketch-geometry (1):
    g0: Circle CenterX=0 CenterY=0 CenterZ=0 NormalX=0 NormalY=0 NormalZ=1 AngleXU=0 Radius=1.9
  constraints (2):
    c: Coincident(g0,g-1)
    c: Radius(g0) = 1.9
FEATURE [PartDesign::Pad] Pad408  label="M3x8 Head046"
  Length = 2
  Length2 = 100
  Profile = -> Sketch1061
  Type = 0
FEATURE [Sketcher::SketchObject] Sketch1063
  MapMode = 5
  Placement = pos=(0,0,2) rot=(0,0,1;0rad)
  Support = -> [Pad415]
  sketch-geometry (1):
    g0: Circle CenterX=0 CenterY=0 CenterZ=0 NormalX=0 NormalY=0 NormalZ=1 AngleXU=0 Radius=1
  constraints (2):
    c: Coincident(g0,g-1)
    c: Radius(g0) = 1
FEATURE [PartDesign::Pad] Pad411  label="M3x8 Thread046"
  BaseFeature = -> Pad415
  Length = 8
  Length2 = 100
  Profile = -> Sketch1063
  Type = 0
FEATURE [Sketcher::SketchObject] Sketch1060
  MapMode = 5
  Placement = pos=(0,0,0) rot=(1,0,0;3.14159rad)
  Support = -> [Pad411]
  sketch-geometry (7):
    g0: LineSegment StartX=0.77 StartY=0.44456 StartZ=0 EndX=0 EndY=0.889119 EndZ=0
    g1: LineSegment StartX=0 StartY=0.889119 StartZ=0 EndX=-0.77 EndY=0.44456 EndZ=0
    g2: LineSegment StartX=-0.77 StartY=0.44456 StartZ=0 EndX=-0.77 EndY=-0.44456 EndZ=0
    g3: LineSegment StartX=-0.77 StartY=-0.44456 StartZ=0 EndX=3.85628e-11 EndY=-0.889119 EndZ=0
    g4: LineSegment StartX=3.85628e-11 StartY=-0.889119 StartZ=0 EndX=0.77 EndY=-0.44456 EndZ=0
    g5: LineSegment StartX=0.77 StartY=-0.44456 StartZ=0 EndX=0.77 EndY=0.44456 EndZ=0
    g6: Circle [constr] CenterX=0 CenterY=0 CenterZ=0 NormalX=0 NormalY=0 NormalZ=1 AngleXU=0 Radius=0.889119
  constraints (16):
    c: Coincident(g0,g1)
    c: Coincident(g1,g2)
    c: Coincident(g2,g3)
    c: Coincident(g3,g4)
    c: Coincident(g4,g5)
    c: Coincident(g5,g0)
    c: Equal(g0, g1-g5) x5
    c: PointOnObject(g0,g6)
    c: PointOnObject(g1,g6)
    c: PointOnObject(g2,g6)
    c: PointOnObject(g3,g6)
    c: PointOnObject(g4,g6)
    c: PointOnObject(g5,g6)
    c: Coincident(g6,g-1)
    c: PointOnObject(g0,g-2)
    c: DistanceX(g1,g0) = 1.54
FEATURE [PartDesign::Pocket] Pocket396  label="M3x8 Wrench052"
  BaseFeature = -> Pad411
  Length = 1
  Length2 = 100
  Profile = -> Sketch1060
  Type = 0
FEATURE [PartDesign::Chamfer] Chamfer170  label="M3x8 Smooth049"
  Base = -> Pocket396 [Face11,Edge2,Edge24,Edge3]
  BaseFeature = -> Pocket396
  Size = 0.2
FEATURE [PartDesign::Body] Body267  label="M2x047"
  Group = -> [Sketch1059,Pad415,Sketch1063,Pad411,Sketch1060,Pocket396,Chamfer170]
  Origin = -> Origin288
  Tip = -> Chamfer170
FEATURE [Sketcher::SketchObject] Sketch1064
  MapMode = 5
  Support = -> [XY_Plane309]
FEATURE [Sketcher::SketchObject] Sketch1066
  MapMode = 5
  Placement = pos=(0,0,2) rot=(0,0,1;0rad)
  Support = -> [Pad413]
  sketch-geometry (1):
    g0: Circle CenterX=0 CenterY=0 CenterZ=0 NormalX=0 NormalY=0 NormalZ=1 AngleXU=0 Radius=1
  constraints (2):
    c: Coincident(g0,g-1)
    c: Radius(g0) = 1
FEATURE [PartDesign::Pad] Pad412  label="M3x8 Thread047"
  BaseFeature = -> Pad413
  Length = 8
  Length2 = 100
  Profile = -> Sketch1066
  Type = 0
FEATURE [Sketcher::SketchObject] Sketch1068
  MapMode = 5
  Support = -> [XY_Plane343]
  sketch-geometry (8):
    g0: LineSegment StartX=0 StartY=2.3094 StartZ=0 EndX=-2 EndY=1.1547 EndZ=0
    g1: LineSegment StartX=-2 StartY=1.1547 StartZ=0 EndX=-2 EndY=-1.1547 EndZ=0
    g2: LineSegment StartX=-2 StartY=-1.1547 StartZ=0 EndX=-2e-16 EndY=-2.3094 EndZ=0
    g3: LineSegment StartX=-2e-16 StartY=-2.3094 StartZ=0 EndX=2 EndY=-1.1547 EndZ=0
    g4: LineSegment StartX=2 StartY=-1.1547 StartZ=0 EndX=2 EndY=1.1547 EndZ=0
    g5: LineSegment StartX=2 StartY=1.1547 StartZ=0 EndX=0 EndY=2.3094 EndZ=0
    g6: Circle [constr] CenterX=0 CenterY=0 CenterZ=0 NormalX=0 NormalY=0 NormalZ=1 AngleXU=0 Radius=2.3094
    g7: Circle CenterX=0 CenterY=0 CenterZ=0 NormalX=0 NormalY=0 NormalZ=1 AngleXU=0 Radius=1
  constraints (18):
    c: Coincident(g0,g1)
    c: Coincident(g1,g2)
    c: Coincident(g2,g3)
    c: Coincident(g3,g4)
    c: Coincident(g4,g5)
    c: Coincident(g5,g0)
    c: Equal(g0, g1-g5) x5
    c: PointOnObject(g0,g6)
    c: PointOnObject(g1,g6)
    c: PointOnObject(g2,g6)
    c: PointOnObject(g3,g6)
    c: PointOnObject(g4,g6)
    c: PointOnObject(g5,g6)
    c: Coincident(g6,g-1)
    c: PointOnObject(g5,g-2)
    c: DistanceX(g0,g4) = 4
    c: Coincident(g7,g-1)
    c: Radius(g7) = 1
FEATURE [PartDesign::Pad] Pad427  label="M3 Nut Primitive080"
  Length = 0.6
  Length2 = 0.6
  Profile = -> Sketch1068
  Type = 4
FEATURE [Sketcher::SketchObject] Sketch1067
  ExternalGeometry = -> [Pad427]
  MapMode = 5
  Placement = pos=(0,0,0) rot=(0.57735,0.57735,0.57735;2.0944rad)
  Support = -> [YZ_Plane369]
  sketch-geometry (6):
    g0: LineSegment StartX=-1.9594 StartY=0.6 StartZ=0 EndX=-2.8094 EndY=0.6 EndZ=0
    g1: LineSegment StartX=-2.8094 StartY=0.6 StartZ=0 EndX=-2.8094 EndY=-0.6 EndZ=0
    g2: LineSegment StartX=-2.8094 StartY=-0.6 StartZ=0 EndX=-1.9594 EndY=-0.6 EndZ=0
    g3: LineSegment StartX=-1.9594 StartY=-0.6 StartZ=0 EndX=-2.3094 EndY=-0.4 EndZ=0
    g4: LineSegment StartX=-2.3094 StartY=-0.4 StartZ=0 EndX=-2.3094 EndY=0.4 EndZ=0
    g5: LineSegment StartX=-2.3094 StartY=0.4 StartZ=0 EndX=-1.9594 EndY=0.6 EndZ=0
  constraints (15):
    c: Horizontal(g0)
    c: Coincident(g0,g1)
    c: Coincident(g1,g2)
    c: Coincident(g2,g3)
    c: Coincident(g3,g4)
    c: Coincident(g4,g5)
    c: Coincident(g5,g0)
    c: Symmetric(g4,g3,g-1)
    c: Symmetric(g0,g2,g-1)
    c: Symmetric(g1,g0,g-1)
    c: DistanceX(g0,g4) = 0.5
    c: DistanceY(g3,g4) = 0.8
    c: DistanceY(g1,g0) = 1.2
    c: PointOnObject(g3,g-3)
    c: DistanceX(g4,g0) = 0.35
FEATURE [PartDesign::Groove] Groove084  label="M3 Nut Smooth080"
  Angle = 360
  Axis = (-2e-16,3e-16,1)
  Base = (0,0,0)
  BaseFeature = -> Pad427
  Profile = -> Sketch1067
  ReferenceAxis = -> Sketch1067 [V_Axis]
  Reversed = true
FEATURE [PartDesign::Chamfer] Chamfer166  label="M3 Nut Smooth Hole068"
  Base = -> Groove084 [Edge24,Edge23]
  BaseFeature = -> Groove084
  Size = 0.2
FEATURE [PartDesign::Body] Body261  label="M2 Nut037"
  Group = -> [Sketch1068,Pad427,Sketch1067,Groove084,Chamfer166,Sketch984,Sketch979]
  Origin = -> Origin298
  Placement = pos=(0,0,2.75) rot=(0,0,1;0rad)
  Tip = -> Chamfer166
FEATURE [App::Part] Part097  label="M037"
  Group = -> [Body267,Body261]
  Origin = -> Origin267
  Placement = pos=(-9.1,-5.25,80) rot=(0,1,0;3.14159rad)
FEATURE [Sketcher::SketchObject] Sketch1070
  MapMode = 5
  Placement = pos=(0,0,0) rot=(1,0,0;3.14159rad)
  Support = -> [Pad412]
  sketch-geometry (7):
    g0: LineSegment StartX=0.77 StartY=0.44456 StartZ=0 EndX=0 EndY=0.889119 EndZ=0
    g1: LineSegment StartX=0 StartY=0.889119 StartZ=0 EndX=-0.77 EndY=0.44456 EndZ=0
    g2: LineSegment StartX=-0.77 StartY=0.44456 StartZ=0 EndX=-0.77 EndY=-0.44456 EndZ=0
    g3: LineSegment StartX=-0.77 StartY=-0.44456 StartZ=0 EndX=3.85628e-11 EndY=-0.889119 EndZ=0
    g4: LineSegment StartX=3.85628e-11 StartY=-0.889119 StartZ=0 EndX=0.77 EndY=-0.44456 EndZ=0
    g5: LineSegment StartX=0.77 StartY=-0.44456 StartZ=0 EndX=0.77 EndY=0.44456 EndZ=0
    g6: Circle [constr] CenterX=0 CenterY=0 CenterZ=0 NormalX=0 NormalY=0 NormalZ=1 AngleXU=0 Radius=0.889119
  constraints (16):
    c: Coincident(g0,g1)
    c: Coincident(g1,g2)
    c: Coincident(g2,g3)
    c: Coincident(g3,g4)
    c: Coincident(g4,g5)
    c: Coincident(g5,g0)
    c: Equal(g0, g1-g5) x5
    c: PointOnObject(g0,g6)
    c: PointOnObject(g1,g6)
    c: PointOnObject(g2,g6)
    c: PointOnObject(g3,g6)
    c: PointOnObject(g4,g6)
    c: PointOnObject(g5,g6)
    c: Coincident(g6,g-1)
    c: PointOnObject(g0,g-2)
    c: DistanceX(g1,g0) = 1.54
FEATURE [PartDesign::Pocket] Pocket391  label="M3x8 Wrench047"
  BaseFeature = -> Pad412
  Length = 1
  Length2 = 100
  Profile = -> Sketch1070
  Type = 0
FEATURE [PartDesign::Chamfer] Chamfer167  label="M3x8 Smooth047"
  Base = -> Pocket391 [Face11,Edge2,Edge24,Edge3]
  BaseFeature = -> Pocket391
  Size = 0.2
FEATURE [PartDesign::Body] Body263  label="M2x045"
  Group = -> [Sketch986,Pad413,Sketch1066,Pad412,Sketch1070,Pocket391,Chamfer167]
  Origin = -> Origin304
  Tip = -> Chamfer167
FEATURE [Sketcher::SketchObject] Sketch1071
  MapMode = 5
  Placement = pos=(0,0,2) rot=(0,0,1;0rad)
  Support = -> [Pad408]
  sketch-geometry (1):
    g0: Circle CenterX=0 CenterY=0 CenterZ=0 NormalX=0 NormalY=0 NormalZ=1 AngleXU=0 Radius=1
  constraints (2):
    c: Coincident(g0,g-1)
    c: Radius(g0) = 1
FEATURE [PartDesign::Pad] Pad433  label="M3x8 Thread053"
  BaseFeature = -> Pad408
  Length = 8
  Length2 = 100
  Profile = -> Sketch1071
  Type = 0
FEATURE [Sketcher::SketchObject] Sketch1072
  MapMode = 5
  Support = -> [XY_Plane349]
  sketch-geometry (8):
    g0: LineSegment StartX=0 StartY=2.3094 StartZ=0 EndX=-2 EndY=1.1547 EndZ=0
    g1: LineSegment StartX=-2 StartY=1.1547 StartZ=0 EndX=-2 EndY=-1.1547 EndZ=0
    g2: LineSegment StartX=-2 StartY=-1.1547 StartZ=0 EndX=-2e-16 EndY=-2.3094 EndZ=0
    g3: LineSegment StartX=-2e-16 StartY=-2.3094 StartZ=0 EndX=2 EndY=-1.1547 EndZ=0
    g4: LineSegment StartX=2 StartY=-1.1547 StartZ=0 EndX=2 EndY=1.1547 EndZ=0
    g5: LineSegment StartX=2 StartY=1.1547 StartZ=0 EndX=0 EndY=2.3094 EndZ=0
    g6: Circle [constr] CenterX=0 CenterY=0 CenterZ=0 NormalX=0 NormalY=0 NormalZ=1 AngleXU=0 Radius=2.3094
    g7: Circle CenterX=0 CenterY=0 CenterZ=0 NormalX=0 NormalY=0 NormalZ=1 AngleXU=0 Radius=1
  constraints (18):
    c: Coincident(g0,g1)
    c: Coincident(g1,g2)
    c: Coincident(g2,g3)
    c: Coincident(g3,g4)
    c: Coincident(g4,g5)
    c: Coincident(g5,g0)
    c: Equal(g0, g1-g5) x5
    c: PointOnObject(g0,g6)
    c: PointOnObject(g1,g6)
    c: PointOnObject(g2,g6)
    c: PointOnObject(g3,g6)
    c: PointOnObject(g4,g6)
    c: PointOnObject(g5,g6)
    c: Coincident(g6,g-1)
    c: PointOnObject(g5,g-2)
    c: DistanceX(g0,g4) = 4
    c: Coincident(g7,g-1)
    c: Radius(g7) = 1
FEATURE [PartDesign::Pad] Pad416  label="M3 Nut Primitive077"
  Length = 0.6
  Length2 = 0.6
  Profile = -> Sketch1072
  Type = 4
FEATURE [Sketcher::SketchObject] Sketch958
  ExternalGeometry = -> [Pad416]
  MapMode = 5
  Placement = pos=(0,0,0) rot=(0.57735,0.57735,0.57735;2.0944rad)
  Support = -> [YZ_Plane348]
  sketch-geometry (6):
    g0: LineSegment StartX=-1.9594 StartY=0.6 StartZ=0 EndX=-2.8094 EndY=0.6 EndZ=0
    g1: LineSegment StartX=-2.8094 StartY=0.6 StartZ=0 EndX=-2.8094 EndY=-0.6 EndZ=0
    g2: LineSegment StartX=-2.8094 StartY=-0.6 StartZ=0 EndX=-1.9594 EndY=-0.6 EndZ=0
    g3: LineSegment StartX=-1.9594 StartY=-0.6 StartZ=0 EndX=-2.3094 EndY=-0.4 EndZ=0
    g4: LineSegment StartX=-2.3094 StartY=-0.4 StartZ=0 EndX=-2.3094 EndY=0.4 EndZ=0
    g5: LineSegment StartX=-2.3094 StartY=0.4 StartZ=0 EndX=-1.9594 EndY=0.6 EndZ=0
  constraints (15):
    c: Horizontal(g0)
    c: Coincident(g0,g1)
    c: Coincident(g1,g2)
    c: Coincident(g2,g3)
    c: Coincident(g3,g4)
    c: Coincident(g4,g5)
    c: Coincident(g5,g0)
    c: Symmetric(g4,g3,g-1)
    c: Symmetric(g0,g2,g-1)
    c: Symmetric(g1,g0,g-1)
    c: DistanceX(g0,g4) = 0.5
    c: DistanceY(g3,g4) = 0.8
    c: DistanceY(g1,g0) = 1.2
    c: PointOnObject(g3,g-3)
    c: DistanceX(g4,g0) = 0.35
FEATURE [PartDesign::Groove] Groove081  label="M3 Nut Smooth077"
  Angle = 360
  Axis = (-2e-16,3e-16,1)
  Base = (0,0,0)
  BaseFeature = -> Pad416
  Profile = -> Sketch958
  ReferenceAxis = -> Sketch958 [V_Axis]
  Reversed = true
FEATURE [PartDesign::Chamfer] Chamfer213  label="M3 Nut Smooth Hole089"
  Base = -> Groove081 [Edge24,Edge23]
  BaseFeature = -> Groove081
  Size = 0.2
FEATURE [PartDesign::Body] Body270  label="M2 Nut039"
  Group = -> [Sketch1072,Pad416,Sketch958,Groove081,Chamfer213,Sketch971,Sketch1057]
  Origin = -> Origin279
  Placement = pos=(0,0,2.75) rot=(0,0,1;0rad)
  Tip = -> Chamfer213
FEATURE [App::Part] Part069  label="M027"
  Group = -> [Body263,Body270]
  Origin = -> Origin301
  Placement = pos=(-9.8e-15,-10.5,80) rot=(0,1,0;3.14159rad)
FEATURE [Sketcher::SketchObject] Sketch1073
  MapMode = 5
  Support = -> [XY_Plane371]
FEATURE [Sketcher::SketchObject] Sketch1074
  MapMode = 5
  Support = -> [XY_Plane371]
FEATURE [Sketcher::SketchObject] Sketch1075
  MapMode = 5
  Placement = pos=(0,0,2) rot=(0,0,1;0rad)
  Support = -> [Pad410]
  sketch-geometry (1):
    g0: Circle CenterX=0 CenterY=0 CenterZ=0 NormalX=0 NormalY=0 NormalZ=1 AngleXU=0 Radius=1
  constraints (2):
    c: Coincident(g0,g-1)
    c: Radius(g0) = 1
FEATURE [PartDesign::Pad] Pad405  label="M3x8 Thread045"
  BaseFeature = -> Pad410
  Length = 8
  Length2 = 100
  Profile = -> Sketch1075
  Type = 0
FEATURE [Sketcher::SketchObject] Sketch1062
  MapMode = 5
  Placement = pos=(0,0,0) rot=(1,0,0;3.14159rad)
  Support = -> [Pad405]
  sketch-geometry (7):
    g0: LineSegment StartX=0.77 StartY=0.44456 StartZ=0 EndX=0 EndY=0.889119 EndZ=0
    g1: LineSegment StartX=0 StartY=0.889119 StartZ=0 EndX=-0.77 EndY=0.44456 EndZ=0
    g2: LineSegment StartX=-0.77 StartY=0.44456 StartZ=0 EndX=-0.77 EndY=-0.44456 EndZ=0
    g3: LineSegment StartX=-0.77 StartY=-0.44456 StartZ=0 EndX=3.85628e-11 EndY=-0.889119 EndZ=0
    g4: LineSegment StartX=3.85628e-11 StartY=-0.889119 StartZ=0 EndX=0.77 EndY=-0.44456 EndZ=0
    g5: LineSegment StartX=0.77 StartY=-0.44456 StartZ=0 EndX=0.77 EndY=0.44456 EndZ=0
    g6: Circle [constr] CenterX=0 CenterY=0 CenterZ=0 NormalX=0 NormalY=0 NormalZ=1 AngleXU=0 Radius=0.889119
  constraints (16):
    c: Coincident(g0,g1)
    c: Coincident(g1,g2)
    c: Coincident(g2,g3)
    c: Coincident(g3,g4)
    c: Coincident(g4,g5)
    c: Coincident(g5,g0)
    c: Equal(g0, g1-g5) x5
    c: PointOnObject(g0,g6)
    c: PointOnObject(g1,g6)
    c: PointOnObject(g2,g6)
    c: PointOnObject(g3,g6)
    c: PointOnObject(g4,g6)
    c: PointOnObject(g5,g6)
    c: Coincident(g6,g-1)
    c: PointOnObject(g0,g-2)
    c: DistanceX(g1,g0) = 1.54
FEATURE [PartDesign::Pocket] Pocket392  label="M3x8 Wrench048"
  BaseFeature = -> Pad405
  Length = 1
  Length2 = 100
  Profile = -> Sketch1062
  Type = 0
FEATURE [PartDesign::Chamfer] Chamfer161  label="M3x8 Smooth044"
  Base = -> Pocket392 [Face11,Edge2,Edge24,Edge3]
  BaseFeature = -> Pocket392
  Size = 0.2
FEATURE [PartDesign::Body] Body264  label="M2x046"
  Group = -> [Sketch992,Pad410,Sketch1075,Pad405,Sketch1062,Pocket392,Chamfer161]
  Origin = -> Origin257
  Placement = pos=(-28.75,10,15) rot=(0,1,0;1.5708rad)
  Tip = -> Chamfer161
FEATURE [Sketcher::SketchObject] Sketch1076
  MapMode = 5
  Support = -> [XY_Plane331]
FEATURE [Sketcher::SketchObject] Sketch1080
  MapMode = 5
  Support = -> [XY_Plane346]
  sketch-geometry (8):
    g0: LineSegment StartX=0 StartY=2.3094 StartZ=0 EndX=-2 EndY=1.1547 EndZ=0
    g1: LineSegment StartX=-2 StartY=1.1547 StartZ=0 EndX=-2 EndY=-1.1547 EndZ=0
    g2: LineSegment StartX=-2 StartY=-1.1547 StartZ=0 EndX=-2e-16 EndY=-2.3094 EndZ=0
    g3: LineSegment StartX=-2e-16 StartY=-2.3094 StartZ=0 EndX=2 EndY=-1.1547 EndZ=0
    g4: LineSegment StartX=2 StartY=-1.1547 StartZ=0 EndX=2 EndY=1.1547 EndZ=0
    g5: LineSegment StartX=2 StartY=1.1547 StartZ=0 EndX=0 EndY=2.3094 EndZ=0
    g6: Circle [constr] CenterX=0 CenterY=0 CenterZ=0 NormalX=0 NormalY=0 NormalZ=1 AngleXU=0 Radius=2.3094
    g7: Circle CenterX=0 CenterY=0 CenterZ=0 NormalX=0 NormalY=0 NormalZ=1 AngleXU=0 Radius=1
  constraints (18):
    c: Coincident(g0,g1)
    c: Coincident(g1,g2)
    c: Coincident(g2,g3)
    c: Coincident(g3,g4)
    c: Coincident(g4,g5)
    c: Coincident(g5,g0)
    c: Equal(g0, g1-g5) x5
    c: PointOnObject(g0,g6)
    c: PointOnObject(g1,g6)
    c: PointOnObject(g2,g6)
    c: PointOnObject(g3,g6)
    c: PointOnObject(g4,g6)
    c: PointOnObject(g5,g6)
    c: Coincident(g6,g-1)
    c: PointOnObject(g5,g-2)
    c: DistanceX(g0,g4) = 4
    c: Coincident(g7,g-1)
    c: Radius(g7) = 1
FEATURE [PartDesign::Pad] Pad437  label="M3 Nut Primitive084"
  Length = 0.6
  Length2 = 0.6
  Profile = -> Sketch1080
  Type = 4
FEATURE [Sketcher::SketchObject] Sketch1000
  ExternalGeometry = -> [Pad437]
  MapMode = 5
  Placement = pos=(0,0,0) rot=(0.57735,0.57735,0.57735;2.0944rad)
  Support = -> [YZ_Plane341]
  sketch-geometry (6):
    g0: LineSegment StartX=-1.9594 StartY=0.6 StartZ=0 EndX=-2.8094 EndY=0.6 EndZ=0
    g1: LineSegment StartX=-2.8094 StartY=0.6 StartZ=0 EndX=-2.8094 EndY=-0.6 EndZ=0
    g2: LineSegment StartX=-2.8094 StartY=-0.6 StartZ=0 EndX=-1.9594 EndY=-0.6 EndZ=0
    g3: LineSegment StartX=-1.9594 StartY=-0.6 StartZ=0 EndX=-2.3094 EndY=-0.4 EndZ=0
    g4: LineSegment StartX=-2.3094 StartY=-0.4 StartZ=0 EndX=-2.3094 EndY=0.4 EndZ=0
    g5: LineSegment StartX=-2.3094 StartY=0.4 StartZ=0 EndX=-1.9594 EndY=0.6 EndZ=0
  constraints (15):
    c: Horizontal(g0)
    c: Coincident(g0,g1)
    c: Coincident(g1,g2)
    c: Coincident(g2,g3)
    c: Coincident(g3,g4)
    c: Coincident(g4,g5)
    c: Coincident(g5,g0)
    c: Symmetric(g4,g3,g-1)
    c: Symmetric(g0,g2,g-1)
    c: Symmetric(g1,g0,g-1)
    c: DistanceX(g0,g4) = 0.5
    c: DistanceY(g3,g4) = 0.8
    c: DistanceY(g1,g0) = 1.2
    c: PointOnObject(g3,g-3)
    c: DistanceX(g4,g0) = 0.35
FEATURE [PartDesign::Groove] Groove088  label="M3 Nut Smooth084"
  Angle = 360
  Axis = (-2e-16,3e-16,1)
  Base = (0,0,0)
  BaseFeature = -> Pad437
  Profile = -> Sketch1000
  ReferenceAxis = -> Sketch1000 [V_Axis]
  Reversed = true
FEATURE [PartDesign::Chamfer] Chamfer153  label="M3 Nut Smooth Hole063"
  Base = -> Groove088 [Edge24,Edge23]
  BaseFeature = -> Groove088
  Size = 0.2
FEATURE [PartDesign::Body] Body244  label="M2 Nut034"
  Group = -> [Sketch1080,Pad437,Sketch1000,Groove088,Chamfer153,Sketch994,Sketch998]
  Origin = -> Origin271
  Placement = pos=(-19.5,10,15) rot=(0.57735,0.57735,-0.57735;4.18879rad)
  Tip = -> Chamfer153
FEATURE [App::Part] Part071  label="SHOULDER PIN001"
  Group = -> [Body244,Body264,Body266]
  Origin = -> Origin299
  Placement = pos=(-3.6e-15,0,30) rot=(0,1,0;3.14159rad)
FEATURE [Sketcher::SketchObject] Sketch1081
  MapMode = 5
  Support = -> [XY_Plane331]
  sketch-geometry (8):
    g0: LineSegment StartX=0 StartY=2.3094 StartZ=0 EndX=-2 EndY=1.1547 EndZ=0
    g1: LineSegment StartX=-2 StartY=1.1547 StartZ=0 EndX=-2 EndY=-1.1547 EndZ=0
    g2: LineSegment StartX=-2 StartY=-1.1547 StartZ=0 EndX=-2e-16 EndY=-2.3094 EndZ=0
    g3: LineSegment StartX=-2e-16 StartY=-2.3094 StartZ=0 EndX=2 EndY=-1.1547 EndZ=0
    g4: LineSegment StartX=2 StartY=-1.1547 StartZ=0 EndX=2 EndY=1.1547 EndZ=0
    g5: LineSegment StartX=2 StartY=1.1547 StartZ=0 EndX=0 EndY=2.3094 EndZ=0
    g6: Circle [constr] CenterX=0 CenterY=0 CenterZ=0 NormalX=0 NormalY=0 NormalZ=1 AngleXU=0 Radius=2.3094
    g7: Circle CenterX=0 CenterY=0 CenterZ=0 NormalX=0 NormalY=0 NormalZ=1 AngleXU=0 Radius=1
  constraints (18):
    c: Coincident(g0,g1)
    c: Coincident(g1,g2)
    c: Coincident(g2,g3)
    c: Coincident(g3,g4)
    c: Coincident(g4,g5)
    c: Coincident(g5,g0)
    c: Equal(g0, g1-g5) x5
    c: PointOnObject(g0,g6)
    c: PointOnObject(g1,g6)
    c: PointOnObject(g2,g6)
    c: PointOnObject(g3,g6)
    c: PointOnObject(g4,g6)
    c: PointOnObject(g5,g6)
    c: Coincident(g6,g-1)
    c: PointOnObject(g5,g-2)
    c: DistanceX(g0,g4) = 4
    c: Coincident(g7,g-1)
    c: Radius(g7) = 1
FEATURE [PartDesign::Pad] Pad420  label="M3 Nut Primitive078"
  Length = 0.6
  Length2 = 0.6
  Profile = -> Sketch1081
  Type = 4
FEATURE [Sketcher::SketchObject] Sketch1079
  ExternalGeometry = -> [Pad420]
  MapMode = 5
  Placement = pos=(0,0,0) rot=(0.57735,0.57735,0.57735;2.0944rad)
  Support = -> [YZ_Plane344]
  sketch-geometry (6):
    g0: LineSegment StartX=-1.9594 StartY=0.6 StartZ=0 EndX=-2.8094 EndY=0.6 EndZ=0
    g1: LineSegment StartX=-2.8094 StartY=0.6 StartZ=0 EndX=-2.8094 EndY=-0.6 EndZ=0
    g2: LineSegment StartX=-2.8094 StartY=-0.6 StartZ=0 EndX=-1.9594 EndY=-0.6 EndZ=0
    g3: LineSegment StartX=-1.9594 StartY=-0.6 StartZ=0 EndX=-2.3094 EndY=-0.4 EndZ=0
    g4: LineSegment StartX=-2.3094 StartY=-0.4 StartZ=0 EndX=-2.3094 EndY=0.4 EndZ=0
    g5: LineSegment StartX=-2.3094 StartY=0.4 StartZ=0 EndX=-1.9594 EndY=0.6 EndZ=0
  constraints (15):
    c: Horizontal(g0)
    c: Coincident(g0,g1)
    c: Coincident(g1,g2)
    c: Coincident(g2,g3)
    c: Coincident(g3,g4)
    c: Coincident(g4,g5)
    c: Coincident(g5,g0)
    c: Symmetric(g4,g3,g-1)
    c: Symmetric(g0,g2,g-1)
    c: Symmetric(g1,g0,g-1)
    c: DistanceX(g0,g4) = 0.5
    c: DistanceY(g3,g4) = 0.8
    c: DistanceY(g1,g0) = 1.2
    c: PointOnObject(g3,g-3)
    c: DistanceX(g4,g0) = 0.35
FEATURE [PartDesign::Groove] Groove089  label="M3 Nut Smooth085"
  Angle = 360
  Axis = (-2e-16,3e-16,1)
  Base = (0,0,0)
  BaseFeature = -> Pad420
  Profile = -> Sketch1079
  ReferenceAxis = -> Sketch1079 [V_Axis]
  Reversed = true
FEATURE [PartDesign::Chamfer] Chamfer169  label="M3 Nut Smooth Hole069"
  Base = -> Groove089 [Edge24,Edge23]
  BaseFeature = -> Groove089
  Size = 0.2
FEATURE [PartDesign::Body] Body269  label="M2 Nut038"
  Group = -> [Sketch1081,Pad420,Sketch1079,Groove089,Chamfer169,Sketch1001,Sketch1076]
  Origin = -> Origin290
  Placement = pos=(0,0,2.75) rot=(0,0,1;0rad)
  Tip = -> Chamfer169
FEATURE [Sketcher::SketchObject] Sketch1082
  MapMode = 5
  Support = -> [XY_Plane372]
  sketch-geometry (1):
    g0: Circle CenterX=0 CenterY=0 CenterZ=0 NormalX=0 NormalY=0 NormalZ=1 AngleXU=0 Radius=1.9
  constraints (2):
    c: Coincident(g0,g-1)
    c: Radius(g0) = 1.9
FEATURE [PartDesign::Pad] Pad432  label="M3x8 Head055"
  Length = 2
  Length2 = 100
  Profile = -> Sketch1082
  Type = 0
FEATURE [Sketcher::SketchObject] Sketch1058
  MapMode = 5
  Placement = pos=(0,0,2) rot=(0,0,1;0rad)
  Support = -> [Pad432]
  sketch-geometry (1):
    g0: Circle CenterX=0 CenterY=0 CenterZ=0 NormalX=0 NormalY=0 NormalZ=1 AngleXU=0 Radius=1
  constraints (2):
    c: Coincident(g0,g-1)
    c: Radius(g0) = 1
FEATURE [PartDesign::Pad] Pad425  label="M3x8 Thread050"
  BaseFeature = -> Pad432
  Length = 8
  Length2 = 100
  Profile = -> Sketch1058
  Type = 0
FEATURE [Sketcher::SketchObject] Sketch1069
  MapMode = 5
  Placement = pos=(0,0,0) rot=(1,0,0;3.14159rad)
  Support = -> [Pad425]
  sketch-geometry (7):
    g0: LineSegment StartX=0.77 StartY=0.44456 StartZ=0 EndX=0 EndY=0.889119 EndZ=0
    g1: LineSegment StartX=0 StartY=0.889119 StartZ=0 EndX=-0.77 EndY=0.44456 EndZ=0
    g2: LineSegment StartX=-0.77 StartY=0.44456 StartZ=0 EndX=-0.77 EndY=-0.44456 EndZ=0
    g3: LineSegment StartX=-0.77 StartY=-0.44456 StartZ=0 EndX=3.85628e-11 EndY=-0.889119 EndZ=0
    g4: LineSegment StartX=3.85628e-11 StartY=-0.889119 StartZ=0 EndX=0.77 EndY=-0.44456 EndZ=0
    g5: LineSegment StartX=0.77 StartY=-0.44456 StartZ=0 EndX=0.77 EndY=0.44456 EndZ=0
    g6: Circle [constr] CenterX=0 CenterY=0 CenterZ=0 NormalX=0 NormalY=0 NormalZ=1 AngleXU=0 Radius=0.889119
  constraints (16):
    c: Coincident(g0,g1)
    c: Coincident(g1,g2)
    c: Coincident(g2,g3)
    c: Coincident(g3,g4)
    c: Coincident(g4,g5)
    c: Coincident(g5,g0)
    c: Equal(g0, g1-g5) x5
    c: PointOnObject(g0,g6)
    c: PointOnObject(g1,g6)
    c: PointOnObject(g2,g6)
    c: PointOnObject(g3,g6)
    c: PointOnObject(g4,g6)
    c: PointOnObject(g5,g6)
    c: Coincident(g6,g-1)
    c: PointOnObject(g0,g-2)
    c: DistanceX(g1,g0) = 1.54
FEATURE [PartDesign::Pocket] Pocket394  label="M3x8 Wrench050"
  BaseFeature = -> Pad425
  Length = 1
  Length2 = 100
  Profile = -> Sketch1069
  Type = 0
FEATURE [PartDesign::Chamfer] Chamfer168  label="M3x8 Smooth048"
  Base = -> Pocket394 [Face11,Edge2,Edge24,Edge3]
  BaseFeature = -> Pocket394
  Size = 0.2
FEATURE [PartDesign::Body] Body262  label="M2x044"
  Group = -> [Sketch1082,Pad432,Sketch1058,Pad425,Sketch1069,Pocket394,Chamfer168]
  Origin = -> Origin259
  Tip = -> Chamfer168
FEATURE [Sketcher::SketchObject] Sketch1083
  MapMode = 5
  Support = -> [XY_Plane309]
FEATURE [Sketcher::SketchObject] Sketch1084
  MapMode = 5
  Support = -> [XY_Plane371]
  sketch-geometry (8):
    g0: LineSegment StartX=0 StartY=2.3094 StartZ=0 EndX=-2 EndY=1.1547 EndZ=0
    g1: LineSegment StartX=-2 StartY=1.1547 StartZ=0 EndX=-2 EndY=-1.1547 EndZ=0
    g2: LineSegment StartX=-2 StartY=-1.1547 StartZ=0 EndX=-2e-16 EndY=-2.3094 EndZ=0
    g3: LineSegment StartX=-2e-16 StartY=-2.3094 StartZ=0 EndX=2 EndY=-1.1547 EndZ=0
    g4: LineSegment StartX=2 StartY=-1.1547 StartZ=0 EndX=2 EndY=1.1547 EndZ=0
    g5: LineSegment StartX=2 StartY=1.1547 StartZ=0 EndX=0 EndY=2.3094 EndZ=0
    g6: Circle [constr] CenterX=0 CenterY=0 CenterZ=0 NormalX=0 NormalY=0 NormalZ=1 AngleXU=0 Radius=2.3094
    g7: Circle CenterX=0 CenterY=0 CenterZ=0 NormalX=0 NormalY=0 NormalZ=1 AngleXU=0 Radius=1
  constraints (18):
    c: Coincident(g0,g1)
    c: Coincident(g1,g2)
    c: Coincident(g2,g3)
    c: Coincident(g3,g4)
    c: Coincident(g4,g5)
    c: Coincident(g5,g0)
    c: Equal(g0, g1-g5) x5
    c: PointOnObject(g0,g6)
    c: PointOnObject(g1,g6)
    c: PointOnObject(g2,g6)
    c: PointOnObject(g3,g6)
    c: PointOnObject(g4,g6)
    c: PointOnObject(g5,g6)
    c: Coincident(g6,g-1)
    c: PointOnObject(g5,g-2)
    c: DistanceX(g0,g4) = 4
    c: Coincident(g7,g-1)
    c: Radius(g7) = 1
FEATURE [PartDesign::Pad] Pad423  label="M3 Nut Primitive079"
  Length = 0.6
  Length2 = 0.6
  Profile = -> Sketch1084
  Type = 4
FEATURE [Sketcher::SketchObject] Sketch1065
  ExternalGeometry = -> [Pad423]
  MapMode = 5
  Placement = pos=(0,0,0) rot=(0.57735,0.57735,0.57735;2.0944rad)
  Support = -> [YZ_Plane373]
  sketch-geometry (6):
    g0: LineSegment StartX=-1.9594 StartY=0.6 StartZ=0 EndX=-2.8094 EndY=0.6 EndZ=0
    g1: LineSegment StartX=-2.8094 StartY=0.6 StartZ=0 EndX=-2.8094 EndY=-0.6 EndZ=0
    g2: LineSegment StartX=-2.8094 StartY=-0.6 StartZ=0 EndX=-1.9594 EndY=-0.6 EndZ=0
    g3: LineSegment StartX=-1.9594 StartY=-0.6 StartZ=0 EndX=-2.3094 EndY=-0.4 EndZ=0
    g4: LineSegment StartX=-2.3094 StartY=-0.4 StartZ=0 EndX=-2.3094 EndY=0.4 EndZ=0
    g5: LineSegment StartX=-2.3094 StartY=0.4 StartZ=0 EndX=-1.9594 EndY=0.6 EndZ=0
  constraints (15):
    c: Horizontal(g0)
    c: Coincident(g0,g1)
    c: Coincident(g1,g2)
    c: Coincident(g2,g3)
    c: Coincident(g3,g4)
    c: Coincident(g4,g5)
    c: Coincident(g5,g0)
    c: Symmetric(g4,g3,g-1)
    c: Symmetric(g0,g2,g-1)
    c: Symmetric(g1,g0,g-1)
    c: DistanceX(g0,g4) = 0.5
    c: DistanceY(g3,g4) = 0.8
    c: DistanceY(g1,g0) = 1.2
    c: PointOnObject(g3,g-3)
    c: DistanceX(g4,g0) = 0.35
FEATURE [PartDesign::Groove] Groove087  label="M3 Nut Smooth083"
  Angle = 360
  Axis = (-2e-16,3e-16,1)
  Base = (0,0,0)
  BaseFeature = -> Pad423
  Profile = -> Sketch1065
  ReferenceAxis = -> Sketch1065 [V_Axis]
  Reversed = true
FEATURE [PartDesign::Chamfer] Chamfer157  label="M3 Nut Smooth Hole065"
  Base = -> Groove087 [Edge24,Edge23]
  BaseFeature = -> Groove087
  Size = 0.2
FEATURE [PartDesign::Body] Body260  label="M2 Nut036"
  Group = -> [Sketch1084,Pad423,Sketch1065,Groove087,Chamfer157,Sketch1073,Sketch1074]
  Origin = -> Origin308
  Placement = pos=(0,0,2.75) rot=(0,0,1;0rad)
  Tip = -> Chamfer157
FEATURE [Sketcher::SketchObject] Sketch1085
  MapMode = 5
  Placement = pos=(0,0,0) rot=(1,0,0;3.14159rad)
  Support = -> [Pad433]
  sketch-geometry (7):
    g0: LineSegment StartX=0.77 StartY=0.44456 StartZ=0 EndX=0 EndY=0.889119 EndZ=0
    g1: LineSegment StartX=0 StartY=0.889119 StartZ=0 EndX=-0.77 EndY=0.44456 EndZ=0
    g2: LineSegment StartX=-0.77 StartY=0.44456 StartZ=0 EndX=-0.77 EndY=-0.44456 EndZ=0
    g3: LineSegment StartX=-0.77 StartY=-0.44456 StartZ=0 EndX=3.85628e-11 EndY=-0.889119 EndZ=0
    g4: LineSegment StartX=3.85628e-11 StartY=-0.889119 StartZ=0 EndX=0.77 EndY=-0.44456 EndZ=0
    g5: LineSegment StartX=0.77 StartY=-0.44456 StartZ=0 EndX=0.77 EndY=0.44456 EndZ=0
    g6: Circle [constr] CenterX=0 CenterY=0 CenterZ=0 NormalX=0 NormalY=0 NormalZ=1 AngleXU=0 Radius=0.889119
  constraints (16):
    c: Coincident(g0,g1)
    c: Coincident(g1,g2)
    c: Coincident(g2,g3)
    c: Coincident(g3,g4)
    c: Coincident(g4,g5)
    c: Coincident(g5,g0)
    c: Equal(g0, g1-g5) x5
    c: PointOnObject(g0,g6)
    c: PointOnObject(g1,g6)
    c: PointOnObject(g2,g6)
    c: PointOnObject(g3,g6)
    c: PointOnObject(g4,g6)
    c: PointOnObject(g5,g6)
    c: Coincident(g6,g-1)
    c: PointOnObject(g0,g-2)
    c: DistanceX(g1,g0) = 1.54
FEATURE [PartDesign::Pocket] Pocket395  label="M3x8 Wrench051"
  BaseFeature = -> Pad433
  Length = 1
  Length2 = 100
  Profile = -> Sketch1085
  Type = 0
FEATURE [PartDesign::Chamfer] Chamfer156  label="M3x8 Smooth042"
  Base = -> Pocket395 [Face11,Edge2,Edge24,Edge3]
  BaseFeature = -> Pocket395
  Size = 0.2
FEATURE [PartDesign::Body] Body238  label="M2x041"
  Group = -> [Sketch1061,Pad408,Sketch1071,Pad433,Sketch1085,Pocket395,Chamfer156]
  Origin = -> Origin285
  Tip = -> Chamfer156
FEATURE [App::Part] Part081  label="M030"
  Group = -> [Body238,Body260]
  Origin = -> Origin268
  Placement = pos=(9.1,5.25,80) rot=(0,1,0;3.14159rad)
FEATURE [Sketcher::SketchObject] Sketch1086
  ExternalGeometry = -> [Pad428]
  MapMode = 5
  Placement = pos=(0,0,0) rot=(0.57735,0.57735,0.57735;2.0944rad)
  Support = -> [YZ_Plane365]
  sketch-geometry (6):
    g0: LineSegment StartX=-1.9594 StartY=0.6 StartZ=0 EndX=-2.8094 EndY=0.6 EndZ=0
    g1: LineSegment StartX=-2.8094 StartY=0.6 StartZ=0 EndX=-2.8094 EndY=-0.6 EndZ=0
    g2: LineSegment StartX=-2.8094 StartY=-0.6 StartZ=0 EndX=-1.9594 EndY=-0.6 EndZ=0
    g3: LineSegment StartX=-1.9594 StartY=-0.6 StartZ=0 EndX=-2.3094 EndY=-0.4 EndZ=0
    g4: LineSegment StartX=-2.3094 StartY=-0.4 StartZ=0 EndX=-2.3094 EndY=0.4 EndZ=0
    g5: LineSegment StartX=-2.3094 StartY=0.4 StartZ=0 EndX=-1.9594 EndY=0.6 EndZ=0
  constraints (15):
    c: Horizontal(g0)
    c: Coincident(g0,g1)
    c: Coincident(g1,g2)
    c: Coincident(g2,g3)
    c: Coincident(g3,g4)
    c: Coincident(g4,g5)
    c: Coincident(g5,g0)
    c: Symmetric(g4,g3,g-1)
    c: Symmetric(g0,g2,g-1)
    c: Symmetric(g1,g0,g-1)
    c: DistanceX(g0,g4) = 0.5
    c: DistanceY(g3,g4) = 0.8
    c: DistanceY(g1,g0) = 1.2
    c: PointOnObject(g3,g-3)
    c: DistanceX(g4,g0) = 0.35
FEATURE [PartDesign::Groove] Groove082  label="M3 Nut Smooth078"
  Angle = 360
  Axis = (-2e-16,3e-16,1)
  Base = (0,0,0)
  BaseFeature = -> Pad428
  Profile = -> Sketch1086
  ReferenceAxis = -> Sketch1086 [V_Axis]
  Reversed = true
FEATURE [PartDesign::Chamfer] Chamfer155  label="M3 Nut Smooth Hole064"
  Base = -> Groove082 [Edge24,Edge23]
  BaseFeature = -> Groove082
  Size = 0.2
FEATURE [PartDesign::Body] Body250  label="M2 Nut035"
  Group = -> [Sketch964,Pad428,Sketch1086,Groove082,Chamfer155,Sketch1064,Sketch1083]
  Origin = -> Origin261
  Placement = pos=(0,0,2.75) rot=(0,0,1;0rad)
  Tip = -> Chamfer155
FEATURE [App::Part] Part067  label="M026"
  Group = -> [Body262,Body250]
  Origin = -> Origin266
  Placement = pos=(9.1,-5.25,80) rot=(0,1,0;3.14159rad)
FEATURE [Sketcher::SketchObject] Sketch1087
  MapMode = 5
  Support = -> [XY_Plane374]
  sketch-geometry (1):
    g0: Circle CenterX=0 CenterY=0 CenterZ=0 NormalX=0 NormalY=0 NormalZ=1 AngleXU=0 Radius=1.9
  constraints (2):
    c: Coincident(g0,g-1)
    c: Radius(g0) = 1.9
FEATURE [PartDesign::Pad] Pad419  label="M3x8 Head051"
  Length = 2
  Length2 = 100
  Profile = -> Sketch1087
  Type = 0
FEATURE [Sketcher::SketchObject] Sketch1078
  MapMode = 5
  Placement = pos=(0,0,2) rot=(0,0,1;0rad)
  Support = -> [Pad419]
  sketch-geometry (1):
    g0: Circle CenterX=0 CenterY=0 CenterZ=0 NormalX=0 NormalY=0 NormalZ=1 AngleXU=0 Radius=1
  constraints (2):
    c: Coincident(g0,g-1)
    c: Radius(g0) = 1
FEATURE [PartDesign::Pad] Pad431  label="M3x8 Thread052"
  BaseFeature = -> Pad419
  Length = 8
  Length2 = 100
  Profile = -> Sketch1078
  Type = 0
FEATURE [Sketcher::SketchObject] Sketch1077
  MapMode = 5
  Placement = pos=(0,0,0) rot=(1,0,0;3.14159rad)
  Support = -> [Pad431]
  sketch-geometry (7):
    g0: LineSegment StartX=0.77 StartY=0.44456 StartZ=0 EndX=0 EndY=0.889119 EndZ=0
    g1: LineSegment StartX=0 StartY=0.889119 StartZ=0 EndX=-0.77 EndY=0.44456 EndZ=0
    g2: LineSegment StartX=-0.77 StartY=0.44456 StartZ=0 EndX=-0.77 EndY=-0.44456 EndZ=0
    g3: LineSegment StartX=-0.77 StartY=-0.44456 StartZ=0 EndX=3.85628e-11 EndY=-0.889119 EndZ=0
    g4: LineSegment StartX=3.85628e-11 StartY=-0.889119 StartZ=0 EndX=0.77 EndY=-0.44456 EndZ=0
    g5: LineSegment StartX=0.77 StartY=-0.44456 StartZ=0 EndX=0.77 EndY=0.44456 EndZ=0
    g6: Circle [constr] CenterX=0 CenterY=0 CenterZ=0 NormalX=0 NormalY=0 NormalZ=1 AngleXU=0 Radius=0.889119
  constraints (16):
    c: Coincident(g0,g1)
    c: Coincident(g1,g2)
    c: Coincident(g2,g3)
    c: Coincident(g3,g4)
    c: Coincident(g4,g5)
    c: Coincident(g5,g0)
    c: Equal(g0, g1-g5) x5
    c: PointOnObject(g0,g6)
    c: PointOnObject(g1,g6)
    c: PointOnObject(g2,g6)
    c: PointOnObject(g3,g6)
    c: PointOnObject(g4,g6)
    c: PointOnObject(g5,g6)
    c: Coincident(g6,g-1)
    c: PointOnObject(g0,g-2)
    c: DistanceX(g1,g0) = 1.54
FEATURE [PartDesign::Pocket] Pocket399  label="M3x8 Wrench053"
  BaseFeature = -> Pad431
  Length = 1
  Length2 = 100
  Profile = -> Sketch1077
  Type = 0
FEATURE [PartDesign::Chamfer] Chamfer214  label="M3x8 Smooth056"
  Base = -> Pocket399 [Face11,Edge2,Edge24,Edge3]
  BaseFeature = -> Pocket399
  Size = 0.2
FEATURE [PartDesign::Body] Body240  label="M2x042"
  Group = -> [Sketch1087,Pad419,Sketch1078,Pad431,Sketch1077,Pocket399,Chamfer214]
  Origin = -> Origin311
  Tip = -> Chamfer214
FEATURE [App::Part] Part073  label="M028"
  Group = -> [Body240,Body269]
  Origin = -> Origin280
  Placement = pos=(-9.1,5.25,80) rot=(0,1,0;3.14159rad)
FEATURE [App::Part] Part075  label="Screws005"
  Group = -> [Part077,Part069,Part097,Part067,Part081,Part073]
  Origin = -> Origin295
  Placement = pos=(0,0,-71) rot=(0,0,1;0rad)
FEATURE [App::Part] Part078  label="Shoulderjoint CAP001"
  Group = -> [Part075,Part070,Body245]
  Origin = -> Origin309
  Placement = pos=(0,0,-12) rot=(0,0,1;0rad)
FEATURE [Sketcher::SketchObject] Sketch1088
  MapMode = 5
  Support = -> [XY_Plane334]
  sketch-geometry (1):
    g0: Circle CenterX=0 CenterY=0 CenterZ=0 NormalX=0 NormalY=0 NormalZ=1 AngleXU=0 Radius=2.75
  constraints (2):
    c: Coincident(g0,g-1)
    c: Radius(g0) = 2.75
FEATURE [PartDesign::Pad] Pad422  label="M3x8 Head053"
  Length = 3
  Length2 = 100
  Profile = -> Sketch1088
  Type = 0
FEATURE [Sketcher::SketchObject] Sketch1013
  MapMode = 5
  Placement = pos=(0,0,3) rot=(0,0,1;0rad)
  Support = -> [Pad422]
  sketch-geometry (1):
    g0: Circle CenterX=0 CenterY=0 CenterZ=0 NormalX=0 NormalY=0 NormalZ=1 AngleXU=0 Radius=1.5
  constraints (2):
    c: Coincident(g0,g-1)
    c: Radius(g0) = 1.5
FEATURE [PartDesign::Pad] Pad430  label="M3x8 Thread051"
  BaseFeature = -> Pad422
  Length = 8
  Length2 = 100
  Profile = -> Sketch1013
  Type = 0
FEATURE [Sketcher::SketchObject] Sketch996
  MapMode = 5
  Placement = pos=(0,0,0) rot=(1,0,0;3.14159rad)
  Support = -> [Pad430]
  sketch-geometry (7):
    g0: LineSegment StartX=1.275 StartY=0.736122 StartZ=0 EndX=0 EndY=1.47224 EndZ=0
    g1: LineSegment StartX=0 StartY=1.47224 StartZ=0 EndX=-1.275 EndY=0.736122 EndZ=0
    g2: LineSegment StartX=-1.275 StartY=0.736122 StartZ=0 EndX=-1.275 EndY=-0.736122 EndZ=0
    g3: LineSegment StartX=-1.275 StartY=-0.736122 StartZ=0 EndX=1.34766e-11 EndY=-1.47224 EndZ=0
    g4: LineSegment StartX=1.34766e-11 StartY=-1.47224 StartZ=0 EndX=1.275 EndY=-0.736122 EndZ=0
    g5: LineSegment StartX=1.275 StartY=-0.736122 StartZ=0 EndX=1.275 EndY=0.736122 EndZ=0
    g6: Circle [constr] CenterX=0 CenterY=0 CenterZ=0 NormalX=0 NormalY=0 NormalZ=1 AngleXU=0 Radius=1.47224
  constraints (16):
    c: Coincident(g0,g1)
    c: Coincident(g1,g2)
    c: Coincident(g2,g3)
    c: Coincident(g3,g4)
    c: Coincident(g4,g5)
    c: Coincident(g5,g0)
    c: Equal(g0, g1-g5) x5
    c: PointOnObject(g0,g6)
    c: PointOnObject(g1,g6)
    c: PointOnObject(g2,g6)
    c: PointOnObject(g3,g6)
    c: PointOnObject(g4,g6)
    c: PointOnObject(g5,g6)
    c: Coincident(g6,g-1)
    c: PointOnObject(g0,g-2)
    c: DistanceX(g1,g0) = 2.55
FEATURE [PartDesign::Pocket] Pocket393  label="M3x8 Wrench049"
  BaseFeature = -> Pad430
  Length = 1.3
  Length2 = 100
  Profile = -> Sketch996
  Type = 0
FEATURE [PartDesign::Chamfer] Chamfer164  label="M3x8 Smooth045"
  Base = -> Pocket393 [Face11,Edge2,Edge24,Edge3]
  BaseFeature = -> Pocket393
  Size = 0.2
FEATURE [PartDesign::Body] Body235  label="M3x056"
  Group = -> [Sketch1088,Pad422,Sketch1013,Pad430,Sketch996,Pocket393,Chamfer164]
  Origin = -> Origin269
  Placement = pos=(14.15,14.15,-6) rot=(0,0,1;0rad)
  Tip = -> Chamfer164
FEATURE [App::Part] Part080  label="Shouldercap Screws001"
  Group = -> [Body235,Body242,Body208,Body237]
  Origin = -> Origin282
FEATURE [Sketcher::SketchObject] Sketch1091
  MapMode = 5
  Placement = pos=(0,0,3) rot=(0,0,1;0rad)
  Support = -> [Pad465]
  sketch-geometry (1):
    g0: Circle CenterX=0 CenterY=0 CenterZ=0 NormalX=0 NormalY=0 NormalZ=1 AngleXU=0 Radius=1.5
  constraints (2):
    c: Coincident(g0,g-1)
    c: Radius(g0) = 1.5
FEATURE [PartDesign::Pad] Pad462  label="M3x20 Thread038"
  BaseFeature = -> Pad465
  Length = 20
  Length2 = 100
  Profile = -> Sketch1091
  Type = 0
FEATURE [Sketcher::SketchObject] Sketch1052
  MapMode = 5
  Placement = pos=(0,0,0) rot=(1,0,0;3.14159rad)
  Support = -> [Pad462]
  sketch-geometry (7):
    g0: LineSegment StartX=1.275 StartY=0.736122 StartZ=0 EndX=0 EndY=1.47224 EndZ=0
    g1: LineSegment StartX=0 StartY=1.47224 StartZ=0 EndX=-1.275 EndY=0.736122 EndZ=0
    g2: LineSegment StartX=-1.275 StartY=0.736122 StartZ=0 EndX=-1.275 EndY=-0.736122 EndZ=0
    g3: LineSegment StartX=-1.275 StartY=-0.736122 StartZ=0 EndX=1.34766e-11 EndY=-1.47224 EndZ=0
    g4: LineSegment StartX=1.34766e-11 StartY=-1.47224 StartZ=0 EndX=1.275 EndY=-0.736122 EndZ=0
    g5: LineSegment StartX=1.275 StartY=-0.736122 StartZ=0 EndX=1.275 EndY=0.736122 EndZ=0
    g6: Circle [constr] CenterX=0 CenterY=0 CenterZ=0 NormalX=0 NormalY=0 NormalZ=1 AngleXU=0 Radius=1.47224
  constraints (16):
    c: Coincident(g0,g1)
    c: Coincident(g1,g2)
    c: Coincident(g2,g3)
    c: Coincident(g3,g4)
    c: Coincident(g4,g5)
    c: Coincident(g5,g0)
    c: Equal(g0, g1-g5) x5
    c: PointOnObject(g0,g6)
    c: PointOnObject(g1,g6)
    c: PointOnObject(g2,g6)
    c: PointOnObject(g3,g6)
    c: PointOnObject(g4,g6)
    c: PointOnObject(g5,g6)
    c: Coincident(g6,g-1)
    c: PointOnObject(g0,g-2)
    c: DistanceX(g1,g0) = 2.55
FEATURE [PartDesign::Pocket] Pocket420  label="M3x20 Wrench037"
  BaseFeature = -> Pad462
  Length = 1.3
  Length2 = 100
  Profile = -> Sketch1052
  Type = 0
FEATURE [PartDesign::Chamfer] Chamfer144  label="M3x20 Smooth026"
  Base = -> Pocket420 [Face11,Edge2,Edge24,Edge3]
  BaseFeature = -> Pocket420
  Size = 0.2
FEATURE [PartDesign::Body] Body268  label="M3x063"
  Group = -> [Sketch1045,Pad465,Sketch1091,Pad462,Sketch1052,Pocket420,Chamfer144]
  Origin = -> Origin294
  Placement = pos=(11.25,-55.6,224.85) rot=(0,-1,0;1.5708rad)
  Tip = -> Chamfer144
FEATURE [Sketcher::SketchObject] Sketch1092
  MapMode = 5
  Support = -> [XY_Plane365]
  sketch-geometry (1):
    g0: Circle CenterX=0 CenterY=0 CenterZ=0 NormalX=0 NormalY=0 NormalZ=1 AngleXU=0 Radius=2.75
  constraints (2):
    c: Coincident(g0,g-1)
    c: Radius(g0) = 2.75
FEATURE [PartDesign::Pad] Pad471  label="M3x20 Head038"
  Length = 3
  Length2 = 100
  Profile = -> Sketch1092
  Type = 0
FEATURE [Sketcher::SketchObject] Sketch1035
  MapMode = 5
  Placement = pos=(0,0,3) rot=(0,0,1;0rad)
  Support = -> [Pad471]
  sketch-geometry (1):
    g0: Circle CenterX=0 CenterY=0 CenterZ=0 NormalX=0 NormalY=0 NormalZ=1 AngleXU=0 Radius=1.5
  constraints (2):
    c: Coincident(g0,g-1)
    c: Radius(g0) = 1.5
FEATURE [PartDesign::Pad] Pad468  label="M3x20 Thread039"
  BaseFeature = -> Pad471
  Length = 20
  Length2 = 100
  Profile = -> Sketch1035
  Type = 0
FEATURE [Sketcher::SketchObject] Sketch1090
  MapMode = 5
  Placement = pos=(0,0,0) rot=(1,0,0;3.14159rad)
  Support = -> [Pad468]
  sketch-geometry (7):
    g0: LineSegment StartX=1.275 StartY=0.736122 StartZ=0 EndX=0 EndY=1.47224 EndZ=0
    g1: LineSegment StartX=0 StartY=1.47224 StartZ=0 EndX=-1.275 EndY=0.736122 EndZ=0
    g2: LineSegment StartX=-1.275 StartY=0.736122 StartZ=0 EndX=-1.275 EndY=-0.736122 EndZ=0
    g3: LineSegment StartX=-1.275 StartY=-0.736122 StartZ=0 EndX=1.34766e-11 EndY=-1.47224 EndZ=0
    g4: LineSegment StartX=1.34766e-11 StartY=-1.47224 StartZ=0 EndX=1.275 EndY=-0.736122 EndZ=0
    g5: LineSegment StartX=1.275 StartY=-0.736122 StartZ=0 EndX=1.275 EndY=0.736122 EndZ=0
    g6: Circle [constr] CenterX=0 CenterY=0 CenterZ=0 NormalX=0 NormalY=0 NormalZ=1 AngleXU=0 Radius=1.47224
  constraints (16):
    c: Coincident(g0,g1)
    c: Coincident(g1,g2)
    c: Coincident(g2,g3)
    c: Coincident(g3,g4)
    c: Coincident(g4,g5)
    c: Coincident(g5,g0)
    c: Equal(g0, g1-g5) x5
    c: PointOnObject(g0,g6)
    c: PointOnObject(g1,g6)
    c: PointOnObject(g2,g6)
    c: PointOnObject(g3,g6)
    c: PointOnObject(g4,g6)
    c: PointOnObject(g5,g6)
    c: Coincident(g6,g-1)
    c: PointOnObject(g0,g-2)
    c: DistanceX(g1,g0) = 2.55
FEATURE [PartDesign::Pocket] Pocket423  label="M3x20 Wrench039"
  BaseFeature = -> Pad468
  Length = 1.3
  Length2 = 100
  Profile = -> Sketch1090
  Type = 0
FEATURE [PartDesign::Chamfer] Chamfer162  label="M3x20 Smooth030"
  Base = -> Pocket423 [Face11,Edge2,Edge24,Edge3]
  BaseFeature = -> Pocket423
  Size = 0.2
FEATURE [PartDesign::Body] Body256  label="M3x060"
  Group = -> [Sketch1092,Pad471,Sketch1035,Pad468,Sketch1090,Pocket423,Chamfer162]
  Origin = -> Origin274
  Placement = pos=(11.3,-65.6,176.35) rot=(0,-1,0;1.5708rad)
  Tip = -> Chamfer162
FEATURE [Sketcher::SketchObject] Sketch1093
  MapMode = 5
  Support = -> [XY_Plane360]
  sketch-geometry (1):
    g0: Circle CenterX=0 CenterY=0 CenterZ=0 NormalX=0 NormalY=0 NormalZ=1 AngleXU=0 Radius=2.75
  constraints (2):
    c: Coincident(g0,g-1)
    c: Radius(g0) = 2.75
FEATURE [PartDesign::Pad] Pad472  label="M3x20 Head039"
  Length = 3
  Length2 = 100
  Profile = -> Sketch1093
  Type = 0
FEATURE [Sketcher::SketchObject] Sketch1094
  MapMode = 5
  Placement = pos=(0,0,3) rot=(0,0,1;0rad)
  Support = -> [Pad472]
  sketch-geometry (1):
    g0: Circle CenterX=0 CenterY=0 CenterZ=0 NormalX=0 NormalY=0 NormalZ=1 AngleXU=0 Radius=1.5
  constraints (2):
    c: Coincident(g0,g-1)
    c: Radius(g0) = 1.5
FEATURE [PartDesign::Pad] Pad457  label="M3x20 Thread037"
  BaseFeature = -> Pad472
  Length = 20
  Length2 = 100
  Profile = -> Sketch1094
  Type = 0
FEATURE [Sketcher::SketchObject] Sketch1089
  MapMode = 5
  Placement = pos=(0,0,0) rot=(1,0,0;3.14159rad)
  Support = -> [Pad457]
  sketch-geometry (7):
    g0: LineSegment StartX=1.275 StartY=0.736122 StartZ=0 EndX=0 EndY=1.47224 EndZ=0
    g1: LineSegment StartX=0 StartY=1.47224 StartZ=0 EndX=-1.275 EndY=0.736122 EndZ=0
    g2: LineSegment StartX=-1.275 StartY=0.736122 StartZ=0 EndX=-1.275 EndY=-0.736122 EndZ=0
    g3: LineSegment StartX=-1.275 StartY=-0.736122 StartZ=0 EndX=1.34766e-11 EndY=-1.47224 EndZ=0
    g4: LineSegment StartX=1.34766e-11 StartY=-1.47224 StartZ=0 EndX=1.275 EndY=-0.736122 EndZ=0
    g5: LineSegment StartX=1.275 StartY=-0.736122 StartZ=0 EndX=1.275 EndY=0.736122 EndZ=0
    g6: Circle [constr] CenterX=0 CenterY=0 CenterZ=0 NormalX=0 NormalY=0 NormalZ=1 AngleXU=0 Radius=1.47224
  constraints (16):
    c: Coincident(g0,g1)
    c: Coincident(g1,g2)
    c: Coincident(g2,g3)
    c: Coincident(g3,g4)
    c: Coincident(g4,g5)
    c: Coincident(g5,g0)
    c: Equal(g0, g1-g5) x5
    c: PointOnObject(g0,g6)
    c: PointOnObject(g1,g6)
    c: PointOnObject(g2,g6)
    c: PointOnObject(g3,g6)
    c: PointOnObject(g4,g6)
    c: PointOnObject(g5,g6)
    c: Coincident(g6,g-1)
    c: PointOnObject(g0,g-2)
    c: DistanceX(g1,g0) = 2.55
FEATURE [PartDesign::Pocket] Pocket419  label="M3x20 Wrench036"
  BaseFeature = -> Pad457
  Length = 1.3
  Length2 = 100
  Profile = -> Sketch1089
  Type = 0
FEATURE [PartDesign::Chamfer] Chamfer145  label="M3x20 Smooth027"
  Base = -> Pocket419 [Face11,Edge2,Edge24,Edge3]
  BaseFeature = -> Pocket419
  Size = 0.2
FEATURE [PartDesign::Body] Body265  label="M3x062"
  Group = -> [Sketch1093,Pad472,Sketch1094,Pad457,Sketch1089,Pocket419,Chamfer145]
  Origin = -> Origin306
  Placement = pos=(11.3,-55.6,176.35) rot=(0,-1,0;1.5708rad)
  Tip = -> Chamfer145
FEATURE [App::Part] Part076  label="Servo Scres001"
  Group = -> [Body257,Body268,Body256,Body265]
  Origin = -> Origin293
FEATURE [Part::Mirroring] Part__Mirroring  label="Shoulder_Joint_Servomount (Mirror #1)"
  Base = (0,0,0)
  Normal = (0,0,1)
  Placement = pos=(0,0,0) rot=(0,1,0;3.14159rad)
  Source = -> Body249
FEATURE [Sketcher::SketchObject] Sketch199
  MapMode = 5
  Placement = pos=(0,0,0) rot=(1,0,0;1.5708rad)
  Support = -> [XZ_Plane040]
  sketch-geometry (8):
    g0: LineSegment StartX=-1.5 StartY=2.25 StartZ=0 EndX=-3.25 EndY=2.25 EndZ=0
    g1: LineSegment StartX=-3.25 StartY=2.25 StartZ=0 EndX=-3.25 EndY=1.25 EndZ=0
    g2: LineSegment StartX=-3.25 StartY=1.25 StartZ=0 EndX=-2 EndY=1.25 EndZ=0
    g3: LineSegment StartX=-2 StartY=1.25 StartZ=0 EndX=-2 EndY=-1.25 EndZ=0
    g4: LineSegment StartX=-2 StartY=-1.25 StartZ=0 EndX=-3.25 EndY=-1.25 EndZ=0
    g5: LineSegment StartX=-3.25 StartY=-1.25 StartZ=0 EndX=-3.25 EndY=-2.25 EndZ=0
    g6: LineSegment StartX=-3.25 StartY=-2.25 StartZ=0 EndX=-1.5 EndY=-2.25 EndZ=0
    g7: LineSegment StartX=-1.5 StartY=-2.25 StartZ=0 EndX=-1.5 EndY=2.25 EndZ=0
  constraints (23):
    c: Horizontal(g0)
    c: Coincident(g0,g1)
    c: Vertical(g1)
    c: Coincident(g1,g2)
    c: Horizontal(g2)
    c: Coincident(g2,g3)
    c: Vertical(g3)
    c: Coincident(g3,g4)
    c: Horizontal(g4)
    c: Coincident(g4,g5)
    c: Vertical(g5)
    c: Coincident(g5,g6)
    c: Horizontal(g6)
    c: Coincident(g6,g7)
    c: Vertical(g7)
    c: Coincident(g0,g7)
    c: Equal(g1,g5)
    c: Symmetric(g4,g1,g-1)
    c: DistanceX(g0,g-1) = 1.5
    c: DistanceY(g3,g3) = 2.5
    c: DistanceY(g7,g7) = 4.5
    c: DistanceX(g0,g-1) = 3.25
    c: DistanceX(g2,g-1) = 2
FEATURE [Sketcher::SketchObject] Sketch709
  MapMode = 5
  Placement = pos=(0,0,0) rot=(1,0,0;1.5708rad)
  Support = -> [XZ_Plane386]
  sketch-geometry (8):
    g0: LineSegment StartX=-1.5 StartY=2.25 StartZ=0 EndX=-3.25 EndY=2.25 EndZ=0
    g1: LineSegment StartX=-3.25 StartY=2.25 StartZ=0 EndX=-3.25 EndY=1.25 EndZ=0
    g2: LineSegment StartX=-3.25 StartY=1.25 StartZ=0 EndX=-2 EndY=1.25 EndZ=0
    g3: LineSegment StartX=-2 StartY=1.25 StartZ=0 EndX=-2 EndY=-1.25 EndZ=0
    g4: LineSegment StartX=-2 StartY=-1.25 StartZ=0 EndX=-3.25 EndY=-1.25 EndZ=0
    g5: LineSegment StartX=-3.25 StartY=-1.25 StartZ=0 EndX=-3.25 EndY=-2.25 EndZ=0
    g6: LineSegment StartX=-3.25 StartY=-2.25 StartZ=0 EndX=-1.5 EndY=-2.25 EndZ=0
    g7: LineSegment StartX=-1.5 StartY=-2.25 StartZ=0 EndX=-1.5 EndY=2.25 EndZ=0
  constraints (23):
    c: Horizontal(g0)
    c: Coincident(g0,g1)
    c: Vertical(g1)
    c: Coincident(g1,g2)
    c: Horizontal(g2)
    c: Coincident(g2,g3)
    c: Vertical(g3)
    c: Coincident(g3,g4)
    c: Horizontal(g4)
    c: Coincident(g4,g5)
    c: Vertical(g5)
    c: Coincident(g5,g6)
    c: Horizontal(g6)
    c: Coincident(g6,g7)
    c: Vertical(g7)
    c: Coincident(g0,g7)
    c: Equal(g1,g5)
    c: Symmetric(g4,g1,g-1)
    c: DistanceX(g0,g-1) = 1.5
    c: DistanceY(g3,g3) = 2.5
    c: DistanceY(g7,g7) = 4.5
    c: DistanceX(g0,g-1) = 3.25
    c: DistanceX(g2,g-1) = 2
FEATURE [Sketcher::SketchObject] Sketch710
  MapMode = 5
  Placement = pos=(0,0,0) rot=(1,0,0;1.5708rad)
  Support = -> [XZ_Plane385]
  sketch-geometry (8):
    g0: LineSegment StartX=-1.5 StartY=2.25 StartZ=0 EndX=-3.25 EndY=2.25 EndZ=0
    g1: LineSegment StartX=-3.25 StartY=2.25 StartZ=0 EndX=-3.25 EndY=1.25 EndZ=0
    g2: LineSegment StartX=-3.25 StartY=1.25 StartZ=0 EndX=-2 EndY=1.25 EndZ=0
    g3: LineSegment StartX=-2 StartY=1.25 StartZ=0 EndX=-2 EndY=-1.25 EndZ=0
    g4: LineSegment StartX=-2 StartY=-1.25 StartZ=0 EndX=-3.25 EndY=-1.25 EndZ=0
    g5: LineSegment StartX=-3.25 StartY=-1.25 StartZ=0 EndX=-3.25 EndY=-2.25 EndZ=0
    g6: LineSegment StartX=-3.25 StartY=-2.25 StartZ=0 EndX=-1.5 EndY=-2.25 EndZ=0
    g7: LineSegment StartX=-1.5 StartY=-2.25 StartZ=0 EndX=-1.5 EndY=2.25 EndZ=0
  constraints (23):
    c: Horizontal(g0)
    c: Coincident(g0,g1)
    c: Vertical(g1)
    c: Coincident(g1,g2)
    c: Horizontal(g2)
    c: Coincident(g2,g3)
    c: Vertical(g3)
    c: Coincident(g3,g4)
    c: Horizontal(g4)
    c: Coincident(g4,g5)
    c: Vertical(g5)
    c: Coincident(g5,g6)
    c: Horizontal(g6)
    c: Coincident(g6,g7)
    c: Vertical(g7)
    c: Coincident(g0,g7)
    c: Equal(g1,g5)
    c: Symmetric(g4,g1,g-1)
    c: DistanceX(g0,g-1) = 1.5
    c: DistanceY(g3,g3) = 2.5
    c: DistanceY(g7,g7) = 4.5
    c: DistanceX(g0,g-1) = 3.25
    c: DistanceX(g2,g-1) = 2
FEATURE [PartDesign::Revolution] Revolution003
  Angle = 360
  Axis = (0,2e-16,1)
  Base = (0,0,0)
  Placement = pos=(0,0,0) rot=(1,0,0;1.5708rad)
  Profile = -> Sketch711
  ReferenceAxis = -> Sketch711 [V_Axis]
FEATURE [PartDesign::Fillet] Fillet129
  Base = -> Revolution003 [Face2,Face6,Edge1,Edge11,Face4]
  BaseFeature = -> Revolution003
  Placement = pos=(0,0,0) rot=(1,0,0;1.5708rad)
  Radius = 0.25
FEATURE [PartDesign::Body] Body274  label="Rubber Dampener003"
  Group = -> [Sketch711,Revolution003,Fillet129]
  Origin = -> Origin392
  Placement = pos=(-62.3,-12.25,93.7) rot=(-1,0,0;1.5708rad)
  Tip = -> Fillet129
FEATURE [PartDesign::Revolution] Revolution
  Angle = 360
  Axis = (0,2e-16,1)
  Base = (0,0,0)
  Placement = pos=(0,0,0) rot=(1,0,0;1.5708rad)
  Profile = -> Sketch199
  ReferenceAxis = -> Sketch199 [V_Axis]
FEATURE [PartDesign::Fillet] Fillet087
  Base = -> Revolution [Face2,Face6,Edge1,Edge11,Face4]
  BaseFeature = -> Revolution
  Placement = pos=(0,0,0) rot=(1,0,0;1.5708rad)
  Radius = 0.25
FEATURE [PartDesign::Body] Body027  label="Rubber Dampener"
  Group = -> [Sketch199,Revolution,Fillet087]
  Origin = -> Origin040
  Placement = pos=(-89.5,-12.25,134.7) rot=(-1,0,0;1.5708rad)
  Tip = -> Fillet087
FEATURE [PartDesign::Revolution] Revolution001
  Angle = 360
  Axis = (0,2e-16,1)
  Base = (0,0,0)
  Placement = pos=(0,0,0) rot=(1,0,0;1.5708rad)
  Profile = -> Sketch709
  ReferenceAxis = -> Sketch709 [V_Axis]
FEATURE [PartDesign::Fillet] Fillet124
  Base = -> Revolution001 [Face2,Face6,Edge1,Edge11,Face4]
  BaseFeature = -> Revolution001
  Placement = pos=(0,0,0) rot=(1,0,0;1.5708rad)
  Radius = 0.25
FEATURE [PartDesign::Body] Body276  label="Rubber Dampener001"
  Group = -> [Sketch709,Revolution001,Fillet124]
  Origin = -> Origin390
  Placement = pos=(-96.5,-12.25,127.7) rot=(-1,0,0;1.5708rad)
  Tip = -> Fillet124
FEATURE [PartDesign::Revolution] Revolution002
  Angle = 360
  Axis = (0,2e-16,1)
  Base = (0,0,0)
  Placement = pos=(0,0,0) rot=(1,0,0;1.5708rad)
  Profile = -> Sketch710
  ReferenceAxis = -> Sketch710 [V_Axis]
FEATURE [PartDesign::Fillet] Fillet126
  Base = -> Revolution002 [Face2,Face6,Edge1,Edge11,Face4]
  BaseFeature = -> Revolution002
  Placement = pos=(0,0,0) rot=(1,0,0;1.5708rad)
  Radius = 0.25
FEATURE [PartDesign::Body] Body272  label="Rubber Dampener002"
  Group = -> [Sketch710,Revolution002,Fillet126]
  Origin = -> Origin391
  Placement = pos=(-55.25,-12.25,100.75) rot=(-1,0,0;1.5708rad)
  Tip = -> Fillet126
FEATURE [App::Part] Part109  label="Rubber Dampeners"
  Group = -> [Body027,Body276,Body272,Body274]
  Origin = -> Origin393
FEATURE [App::Part] Part096  label="RL Lower Leg"
  Group = -> [Part107,Part105,Part084,Part085,Part090,Part104,Part109]
  Origin = -> Origin365
  Placement = pos=(-0.0178536,0,0.205627) rot=(0,0,1;0rad)
FEATURE [Sketcher::SketchObject] Sketch1095
  MapMode = 5
  Placement = pos=(0,0,0) rot=(1,0,0;1.5708rad)
  Support = -> [XZ_Plane391]
  sketch-geometry (8):
    g0: LineSegment StartX=-1.5 StartY=2.25 StartZ=0 EndX=-3.25 EndY=2.25 EndZ=0
    g1: LineSegment StartX=-3.25 StartY=2.25 StartZ=0 EndX=-3.25 EndY=1.25 EndZ=0
    g2: LineSegment StartX=-3.25 StartY=1.25 StartZ=0 EndX=-2 EndY=1.25 EndZ=0
    g3: LineSegment StartX=-2 StartY=1.25 StartZ=0 EndX=-2 EndY=-1.25 EndZ=0
    g4: LineSegment StartX=-2 StartY=-1.25 StartZ=0 EndX=-3.25 EndY=-1.25 EndZ=0
    g5: LineSegment StartX=-3.25 StartY=-1.25 StartZ=0 EndX=-3.25 EndY=-2.25 EndZ=0
    g6: LineSegment StartX=-3.25 StartY=-2.25 StartZ=0 EndX=-1.5 EndY=-2.25 EndZ=0
    g7: LineSegment StartX=-1.5 StartY=-2.25 StartZ=0 EndX=-1.5 EndY=2.25 EndZ=0
  constraints (23):
    c: Horizontal(g0)
    c: Coincident(g0,g1)
    c: Vertical(g1)
    c: Coincident(g1,g2)
    c: Horizontal(g2)
    c: Coincident(g2,g3)
    c: Vertical(g3)
    c: Coincident(g3,g4)
    c: Horizontal(g4)
    c: Coincident(g4,g5)
    c: Vertical(g5)
    c: Coincident(g5,g6)
    c: Horizontal(g6)
    c: Coincident(g6,g7)
    c: Vertical(g7)
    c: Coincident(g0,g7)
    c: Equal(g1,g5)
    c: Symmetric(g4,g1,g-1)
    c: DistanceX(g0,g-1) = 1.5
    c: DistanceY(g3,g3) = 2.5
    c: DistanceY(g7,g7) = 4.5
    c: DistanceX(g0,g-1) = 3.25
    c: DistanceX(g2,g-1) = 2
FEATURE [PartDesign::Revolution] Revolution004
  Angle = 360
  Axis = (0,2e-16,1)
  Base = (0,0,0)
  Placement = pos=(0,0,0) rot=(1,0,0;1.5708rad)
  Profile = -> Sketch1095
  ReferenceAxis = -> Sketch1095 [V_Axis]
FEATURE [PartDesign::Fillet] Fillet133
  Base = -> Revolution004 [Face2,Face6,Edge1,Edge11,Face4]
  BaseFeature = -> Revolution004
  Placement = pos=(0,0,0) rot=(1,0,0;1.5708rad)
  Radius = 0.25
FEATURE [PartDesign::Body] Body278  label="Rubber Dampener005"
  Group = -> [Sketch1095,Revolution004,Fillet133]
  Origin = -> Origin386
  Placement = pos=(-62.3,-12.25,93.7) rot=(-1,0,0;1.5708rad)
  Tip = -> Fillet133
FEATURE [Sketcher::SketchObject] Sketch1096
  MapMode = 5
  Placement = pos=(0,0,0) rot=(1,0,0;1.5708rad)
  Support = -> [XZ_Plane393]
  sketch-geometry (8):
    g0: LineSegment StartX=-1.5 StartY=2.25 StartZ=0 EndX=-3.25 EndY=2.25 EndZ=0
    g1: LineSegment StartX=-3.25 StartY=2.25 StartZ=0 EndX=-3.25 EndY=1.25 EndZ=0
    g2: LineSegment StartX=-3.25 StartY=1.25 StartZ=0 EndX=-2 EndY=1.25 EndZ=0
    g3: LineSegment StartX=-2 StartY=1.25 StartZ=0 EndX=-2 EndY=-1.25 EndZ=0
    g4: LineSegment StartX=-2 StartY=-1.25 StartZ=0 EndX=-3.25 EndY=-1.25 EndZ=0
    g5: LineSegment StartX=-3.25 StartY=-1.25 StartZ=0 EndX=-3.25 EndY=-2.25 EndZ=0
    g6: LineSegment StartX=-3.25 StartY=-2.25 StartZ=0 EndX=-1.5 EndY=-2.25 EndZ=0
    g7: LineSegment StartX=-1.5 StartY=-2.25 StartZ=0 EndX=-1.5 EndY=2.25 EndZ=0
  constraints (23):
    c: Horizontal(g0)
    c: Coincident(g0,g1)
    c: Vertical(g1)
    c: Coincident(g1,g2)
    c: Horizontal(g2)
    c: Coincident(g2,g3)
    c: Vertical(g3)
    c: Coincident(g3,g4)
    c: Horizontal(g4)
    c: Coincident(g4,g5)
    c: Vertical(g5)
    c: Coincident(g5,g6)
    c: Horizontal(g6)
    c: Coincident(g6,g7)
    c: Vertical(g7)
    c: Coincident(g0,g7)
    c: Equal(g1,g5)
    c: Symmetric(g4,g1,g-1)
    c: DistanceX(g0,g-1) = 1.5
    c: DistanceY(g3,g3) = 2.5
    c: DistanceY(g7,g7) = 4.5
    c: DistanceX(g0,g-1) = 3.25
    c: DistanceX(g2,g-1) = 2
FEATURE [PartDesign::Revolution] Revolution005
  Angle = 360
  Axis = (0,2e-16,1)
  Base = (0,0,0)
  Placement = pos=(0,0,0) rot=(1,0,0;1.5708rad)
  Profile = -> Sketch1096
  ReferenceAxis = -> Sketch1096 [V_Axis]
FEATURE [PartDesign::Fillet] Fillet131
  Base = -> Revolution005 [Face2,Face6,Edge1,Edge11,Face4]
  BaseFeature = -> Revolution005
  Placement = pos=(0,0,0) rot=(1,0,0;1.5708rad)
  Radius = 0.25
FEATURE [PartDesign::Body] Body281  label="Rubber Dampener006"
  Group = -> [Sketch1096,Revolution005,Fillet131]
  Origin = -> Origin396
  Placement = pos=(-89.5,-12.25,134.7) rot=(-1,0,0;1.5708rad)
  Tip = -> Fillet131
FEATURE [Sketcher::SketchObject] Sketch1097
  MapMode = 5
  Placement = pos=(0,0,0) rot=(1,0,0;1.5708rad)
  Support = -> [XZ_Plane389]
  sketch-geometry (8):
    g0: LineSegment StartX=-1.5 StartY=2.25 StartZ=0 EndX=-3.25 EndY=2.25 EndZ=0
    g1: LineSegment StartX=-3.25 StartY=2.25 StartZ=0 EndX=-3.25 EndY=1.25 EndZ=0
    g2: LineSegment StartX=-3.25 StartY=1.25 StartZ=0 EndX=-2 EndY=1.25 EndZ=0
    g3: LineSegment StartX=-2 StartY=1.25 StartZ=0 EndX=-2 EndY=-1.25 EndZ=0
    g4: LineSegment StartX=-2 StartY=-1.25 StartZ=0 EndX=-3.25 EndY=-1.25 EndZ=0
    g5: LineSegment StartX=-3.25 StartY=-1.25 StartZ=0 EndX=-3.25 EndY=-2.25 EndZ=0
    g6: LineSegment StartX=-3.25 StartY=-2.25 StartZ=0 EndX=-1.5 EndY=-2.25 EndZ=0
    g7: LineSegment StartX=-1.5 StartY=-2.25 StartZ=0 EndX=-1.5 EndY=2.25 EndZ=0
  constraints (23):
    c: Horizontal(g0)
    c: Coincident(g0,g1)
    c: Vertical(g1)
    c: Coincident(g1,g2)
    c: Horizontal(g2)
    c: Coincident(g2,g3)
    c: Vertical(g3)
    c: Coincident(g3,g4)
    c: Horizontal(g4)
    c: Coincident(g4,g5)
    c: Vertical(g5)
    c: Coincident(g5,g6)
    c: Horizontal(g6)
    c: Coincident(g6,g7)
    c: Vertical(g7)
    c: Coincident(g0,g7)
    c: Equal(g1,g5)
    c: Symmetric(g4,g1,g-1)
    c: DistanceX(g0,g-1) = 1.5
    c: DistanceY(g3,g3) = 2.5
    c: DistanceY(g7,g7) = 4.5
    c: DistanceX(g0,g-1) = 3.25
    c: DistanceX(g2,g-1) = 2
FEATURE [PartDesign::Revolution] Revolution006
  Angle = 360
  Axis = (0,2e-16,1)
  Base = (0,0,0)
  Placement = pos=(0,0,0) rot=(1,0,0;1.5708rad)
  Profile = -> Sketch1097
  ReferenceAxis = -> Sketch1097 [V_Axis]
FEATURE [PartDesign::Fillet] Fillet132
  Base = -> Revolution006 [Face2,Face6,Edge1,Edge11,Face4]
  BaseFeature = -> Revolution006
  Placement = pos=(0,0,0) rot=(1,0,0;1.5708rad)
  Radius = 0.25
FEATURE [PartDesign::Body] Body280  label="Rubber Dampener007"
  Group = -> [Sketch1097,Revolution006,Fillet132]
  Origin = -> Origin394
  Placement = pos=(-96.5,-12.25,127.7) rot=(-1,0,0;1.5708rad)
  Tip = -> Fillet132
FEATURE [Sketcher::SketchObject] Sketch1098
  MapMode = 5
  Placement = pos=(0,0,0) rot=(1,0,0;1.5708rad)
  Support = -> [XZ_Plane384]
  sketch-geometry (8):
    g0: LineSegment StartX=-1.5 StartY=2.25 StartZ=0 EndX=-3.25 EndY=2.25 EndZ=0
    g1: LineSegment StartX=-3.25 StartY=2.25 StartZ=0 EndX=-3.25 EndY=1.25 EndZ=0
    g2: LineSegment StartX=-3.25 StartY=1.25 StartZ=0 EndX=-2 EndY=1.25 EndZ=0
    g3: LineSegment StartX=-2 StartY=1.25 StartZ=0 EndX=-2 EndY=-1.25 EndZ=0
    g4: LineSegment StartX=-2 StartY=-1.25 StartZ=0 EndX=-3.25 EndY=-1.25 EndZ=0
    g5: LineSegment StartX=-3.25 StartY=-1.25 StartZ=0 EndX=-3.25 EndY=-2.25 EndZ=0
    g6: LineSegment StartX=-3.25 StartY=-2.25 StartZ=0 EndX=-1.5 EndY=-2.25 EndZ=0
    g7: LineSegment StartX=-1.5 StartY=-2.25 StartZ=0 EndX=-1.5 EndY=2.25 EndZ=0
  constraints (23):
    c: Horizontal(g0)
    c: Coincident(g0,g1)
    c: Vertical(g1)
    c: Coincident(g1,g2)
    c: Horizontal(g2)
    c: Coincident(g2,g3)
    c: Vertical(g3)
    c: Coincident(g3,g4)
    c: Horizontal(g4)
    c: Coincident(g4,g5)
    c: Vertical(g5)
    c: Coincident(g5,g6)
    c: Horizontal(g6)
    c: Coincident(g6,g7)
    c: Vertical(g7)
    c: Coincident(g0,g7)
    c: Equal(g1,g5)
    c: Symmetric(g4,g1,g-1)
    c: DistanceX(g0,g-1) = 1.5
    c: DistanceY(g3,g3) = 2.5
    c: DistanceY(g7,g7) = 4.5
    c: DistanceX(g0,g-1) = 3.25
    c: DistanceX(g2,g-1) = 2
FEATURE [PartDesign::Revolution] Revolution007
  Angle = 360
  Axis = (0,2e-16,1)
  Base = (0,0,0)
  Placement = pos=(0,0,0) rot=(1,0,0;1.5708rad)
  Profile = -> Sketch1098
  ReferenceAxis = -> Sketch1098 [V_Axis]
FEATURE [PartDesign::Fillet] Fillet130
  Base = -> Revolution007 [Face2,Face6,Edge1,Edge11,Face4]
  BaseFeature = -> Revolution007
  Placement = pos=(0,0,0) rot=(1,0,0;1.5708rad)
  Radius = 0.25
FEATURE [PartDesign::Body] Body273  label="Rubber Dampener004"
  Group = -> [Sketch1098,Revolution007,Fillet130]
  Origin = -> Origin395
  Placement = pos=(-55.25,-12.25,100.75) rot=(-1,0,0;1.5708rad)
  Tip = -> Fillet130
FEATURE [App::Part] Part110  label="Rubber Dampeners001"
  Group = -> [Body281,Body280,Body273,Body278]
  Origin = -> Origin387
  Placement = pos=(87.2923,-8.85,29.8753) rot=(0,1,0;5.49779rad)
FEATURE [App::Part] Part099  label="RL Upper Leg"
  Group = -> [Part082,Part092,Body195,Body230,Part100,Part106,Part095,Part101,Part102,Part103,Body198,Part110]
  Origin = -> Origin324
  Placement = pos=(55.5497,0.15,169.885) rot=(0,1,0;5.75959rad)
FEATURE [Sketcher::SketchObject] Sketch1099
  MapMode = 5
  Placement = pos=(0,0,0) rot=(1,0,0;1.5708rad)
  Support = -> [XZ_Plane396]
  sketch-geometry (8):
    g0: LineSegment StartX=-1.5 StartY=2.25 StartZ=0 EndX=-3.25 EndY=2.25 EndZ=0
    g1: LineSegment StartX=-3.25 StartY=2.25 StartZ=0 EndX=-3.25 EndY=1.25 EndZ=0
    g2: LineSegment StartX=-3.25 StartY=1.25 StartZ=0 EndX=-2 EndY=1.25 EndZ=0
    g3: LineSegment StartX=-2 StartY=1.25 StartZ=0 EndX=-2 EndY=-1.25 EndZ=0
    g4: LineSegment StartX=-2 StartY=-1.25 StartZ=0 EndX=-3.25 EndY=-1.25 EndZ=0
    g5: LineSegment StartX=-3.25 StartY=-1.25 StartZ=0 EndX=-3.25 EndY=-2.25 EndZ=0
    g6: LineSegment StartX=-3.25 StartY=-2.25 StartZ=0 EndX=-1.5 EndY=-2.25 EndZ=0
    g7: LineSegment StartX=-1.5 StartY=-2.25 StartZ=0 EndX=-1.5 EndY=2.25 EndZ=0
  constraints (23):
    c: Horizontal(g0)
    c: Coincident(g0,g1)
    c: Vertical(g1)
    c: Coincident(g1,g2)
    c: Horizontal(g2)
    c: Coincident(g2,g3)
    c: Vertical(g3)
    c: Coincident(g3,g4)
    c: Horizontal(g4)
    c: Coincident(g4,g5)
    c: Vertical(g5)
    c: Coincident(g5,g6)
    c: Horizontal(g6)
    c: Coincident(g6,g7)
    c: Vertical(g7)
    c: Coincident(g0,g7)
    c: Equal(g1,g5)
    c: Symmetric(g4,g1,g-1)
    c: DistanceX(g0,g-1) = 1.5
    c: DistanceY(g3,g3) = 2.5
    c: DistanceY(g7,g7) = 4.5
    c: DistanceX(g0,g-1) = 3.25
    c: DistanceX(g2,g-1) = 2
FEATURE [PartDesign::Revolution] Revolution009
  Angle = 360
  Axis = (0,2e-16,1)
  Base = (0,0,0)
  Placement = pos=(0,0,0) rot=(1,0,0;1.5708rad)
  Profile = -> Sketch1099
  ReferenceAxis = -> Sketch1099 [V_Axis]
FEATURE [PartDesign::Fillet] Fillet128
  Base = -> Revolution009 [Face2,Face6,Edge1,Edge11,Face4]
  BaseFeature = -> Revolution009
  Placement = pos=(0,0,0) rot=(1,0,0;1.5708rad)
  Radius = 0.25
FEATURE [PartDesign::Body] Body277  label="Rubber Dampener009"
  Group = -> [Sketch1099,Revolution009,Fillet128]
  Origin = -> Origin389
  Placement = pos=(-62.3,-12.25,93.7) rot=(-1,0,0;1.5708rad)
  Tip = -> Fillet128
FEATURE [Sketcher::SketchObject] Sketch1100
  MapMode = 5
  Placement = pos=(0,0,0) rot=(1,0,0;1.5708rad)
  Support = -> [XZ_Plane390]
  sketch-geometry (8):
    g0: LineSegment StartX=-1.5 StartY=2.25 StartZ=0 EndX=-3.25 EndY=2.25 EndZ=0
    g1: LineSegment StartX=-3.25 StartY=2.25 StartZ=0 EndX=-3.25 EndY=1.25 EndZ=0
    g2: LineSegment StartX=-3.25 StartY=1.25 StartZ=0 EndX=-2 EndY=1.25 EndZ=0
    g3: LineSegment StartX=-2 StartY=1.25 StartZ=0 EndX=-2 EndY=-1.25 EndZ=0
    g4: LineSegment StartX=-2 StartY=-1.25 StartZ=0 EndX=-3.25 EndY=-1.25 EndZ=0
    g5: LineSegment StartX=-3.25 StartY=-1.25 StartZ=0 EndX=-3.25 EndY=-2.25 EndZ=0
    g6: LineSegment StartX=-3.25 StartY=-2.25 StartZ=0 EndX=-1.5 EndY=-2.25 EndZ=0
    g7: LineSegment StartX=-1.5 StartY=-2.25 StartZ=0 EndX=-1.5 EndY=2.25 EndZ=0
  constraints (23):
    c: Horizontal(g0)
    c: Coincident(g0,g1)
    c: Vertical(g1)
    c: Coincident(g1,g2)
    c: Horizontal(g2)
    c: Coincident(g2,g3)
    c: Vertical(g3)
    c: Coincident(g3,g4)
    c: Horizontal(g4)
    c: Coincident(g4,g5)
    c: Vertical(g5)
    c: Coincident(g5,g6)
    c: Horizontal(g6)
    c: Coincident(g6,g7)
    c: Vertical(g7)
    c: Coincident(g0,g7)
    c: Equal(g1,g5)
    c: Symmetric(g4,g1,g-1)
    c: DistanceX(g0,g-1) = 1.5
    c: DistanceY(g3,g3) = 2.5
    c: DistanceY(g7,g7) = 4.5
    c: DistanceX(g0,g-1) = 3.25
    c: DistanceX(g2,g-1) = 2
FEATURE [PartDesign::Revolution] Revolution010
  Angle = 360
  Axis = (0,2e-16,1)
  Base = (0,0,0)
  Placement = pos=(0,0,0) rot=(1,0,0;1.5708rad)
  Profile = -> Sketch1100
  ReferenceAxis = -> Sketch1100 [V_Axis]
FEATURE [PartDesign::Fillet] Fillet127
  Base = -> Revolution010 [Face2,Face6,Edge1,Edge11,Face4]
  BaseFeature = -> Revolution010
  Placement = pos=(0,0,0) rot=(1,0,0;1.5708rad)
  Radius = 0.25
FEATURE [PartDesign::Body] Body282  label="Rubber Dampener011"
  Group = -> [Sketch1100,Revolution010,Fillet127]
  Origin = -> Origin384
  Placement = pos=(-89.5,-12.25,134.7) rot=(-1,0,0;1.5708rad)
  Tip = -> Fillet127
FEATURE [Sketcher::SketchObject] Sketch1101
  MapMode = 5
  Placement = pos=(0,0,0) rot=(1,0,0;1.5708rad)
  Support = -> [XZ_Plane394]
  sketch-geometry (8):
    g0: LineSegment StartX=-1.5 StartY=2.25 StartZ=0 EndX=-3.25 EndY=2.25 EndZ=0
    g1: LineSegment StartX=-3.25 StartY=2.25 StartZ=0 EndX=-3.25 EndY=1.25 EndZ=0
    g2: LineSegment StartX=-3.25 StartY=1.25 StartZ=0 EndX=-2 EndY=1.25 EndZ=0
    g3: LineSegment StartX=-2 StartY=1.25 StartZ=0 EndX=-2 EndY=-1.25 EndZ=0
    g4: LineSegment StartX=-2 StartY=-1.25 StartZ=0 EndX=-3.25 EndY=-1.25 EndZ=0
    g5: LineSegment StartX=-3.25 StartY=-1.25 StartZ=0 EndX=-3.25 EndY=-2.25 EndZ=0
    g6: LineSegment StartX=-3.25 StartY=-2.25 StartZ=0 EndX=-1.5 EndY=-2.25 EndZ=0
    g7: LineSegment StartX=-1.5 StartY=-2.25 StartZ=0 EndX=-1.5 EndY=2.25 EndZ=0
  constraints (23):
    c: Horizontal(g0)
    c: Coincident(g0,g1)
    c: Vertical(g1)
    c: Coincident(g1,g2)
    c: Horizontal(g2)
    c: Coincident(g2,g3)
    c: Vertical(g3)
    c: Coincident(g3,g4)
    c: Horizontal(g4)
    c: Coincident(g4,g5)
    c: Vertical(g5)
    c: Coincident(g5,g6)
    c: Horizontal(g6)
    c: Coincident(g6,g7)
    c: Vertical(g7)
    c: Coincident(g0,g7)
    c: Equal(g1,g5)
    c: Symmetric(g4,g1,g-1)
    c: DistanceX(g0,g-1) = 1.5
    c: DistanceY(g3,g3) = 2.5
    c: DistanceY(g7,g7) = 4.5
    c: DistanceX(g0,g-1) = 3.25
    c: DistanceX(g2,g-1) = 2
FEATURE [PartDesign::Revolution] Revolution008
  Angle = 360
  Axis = (0,2e-16,1)
  Base = (0,0,0)
  Placement = pos=(0,0,0) rot=(1,0,0;1.5708rad)
  Profile = -> Sketch1101
  ReferenceAxis = -> Sketch1101 [V_Axis]
FEATURE [PartDesign::Fillet] Fillet123
  Base = -> Revolution008 [Face2,Face6,Edge1,Edge11,Face4]
  BaseFeature = -> Revolution008
  Placement = pos=(0,0,0) rot=(1,0,0;1.5708rad)
  Radius = 0.25
FEATURE [PartDesign::Body] Body275  label="Rubber Dampener008"
  Group = -> [Sketch1101,Revolution008,Fillet123]
  Origin = -> Origin388
  Placement = pos=(-55.25,-12.25,100.75) rot=(-1,0,0;1.5708rad)
  Tip = -> Fillet123
FEATURE [Sketcher::SketchObject] Sketch1102
  MapMode = 5
  Placement = pos=(0,0,0) rot=(1,0,0;1.5708rad)
  Support = -> [XZ_Plane395]
  sketch-geometry (8):
    g0: LineSegment StartX=-1.5 StartY=2.25 StartZ=0 EndX=-3.25 EndY=2.25 EndZ=0
    g1: LineSegment StartX=-3.25 StartY=2.25 StartZ=0 EndX=-3.25 EndY=1.25 EndZ=0
    g2: LineSegment StartX=-3.25 StartY=1.25 StartZ=0 EndX=-2 EndY=1.25 EndZ=0
    g3: LineSegment StartX=-2 StartY=1.25 StartZ=0 EndX=-2 EndY=-1.25 EndZ=0
    g4: LineSegment StartX=-2 StartY=-1.25 StartZ=0 EndX=-3.25 EndY=-1.25 EndZ=0
    g5: LineSegment StartX=-3.25 StartY=-1.25 StartZ=0 EndX=-3.25 EndY=-2.25 EndZ=0
    g6: LineSegment StartX=-3.25 StartY=-2.25 StartZ=0 EndX=-1.5 EndY=-2.25 EndZ=0
    g7: LineSegment StartX=-1.5 StartY=-2.25 StartZ=0 EndX=-1.5 EndY=2.25 EndZ=0
  constraints (23):
    c: Horizontal(g0)
    c: Coincident(g0,g1)
    c: Vertical(g1)
    c: Coincident(g1,g2)
    c: Horizontal(g2)
    c: Coincident(g2,g3)
    c: Vertical(g3)
    c: Coincident(g3,g4)
    c: Horizontal(g4)
    c: Coincident(g4,g5)
    c: Vertical(g5)
    c: Coincident(g5,g6)
    c: Horizontal(g6)
    c: Coincident(g6,g7)
    c: Vertical(g7)
    c: Coincident(g0,g7)
    c: Equal(g1,g5)
    c: Symmetric(g4,g1,g-1)
    c: DistanceX(g0,g-1) = 1.5
    c: DistanceY(g3,g3) = 2.5
    c: DistanceY(g7,g7) = 4.5
    c: DistanceX(g0,g-1) = 3.25
    c: DistanceX(g2,g-1) = 2
FEATURE [PartDesign::Revolution] Revolution011
  Angle = 360
  Axis = (0,2e-16,1)
  Base = (0,0,0)
  Placement = pos=(0,0,0) rot=(1,0,0;1.5708rad)
  Profile = -> Sketch1102
  ReferenceAxis = -> Sketch1102 [V_Axis]
FEATURE [PartDesign::Fillet] Fillet125
  Base = -> Revolution011 [Face2,Face6,Edge1,Edge11,Face4]
  BaseFeature = -> Revolution011
  Placement = pos=(0,0,0) rot=(1,0,0;1.5708rad)
  Radius = 0.25
FEATURE [PartDesign::Body] Body279  label="Rubber Dampener010"
  Group = -> [Sketch1102,Revolution011,Fillet125]
  Origin = -> Origin383
  Placement = pos=(-96.5,-12.25,127.7) rot=(-1,0,0;1.5708rad)
  Tip = -> Fillet125
FEATURE [App::Part] Part108  label="Rubber Dampeners002"
  Group = -> [Body282,Body279,Body275,Body277]
  Origin = -> Origin385
  Placement = pos=(18.7923,-33.3866,66.0791) rot=(0.357407,0.357407,-0.862856;1.71777rad)
FEATURE [App::Part] Part079  label="FL Shoulder Joint Servo001"
  Group = -> [Part098,Body247,Body252,Body255,Body246,Part076,Part108]
  Origin = -> Origin314
  Placement = pos=(-5.4,-200.45,76.1) rot=(0,0.707107,0.707107;3.14159rad)
FEATURE [App::Part] Part068  label="RL Shoulder Joint"
  Group = -> [Body249,Part078,Part071,Part074,Part080,Body254,Part__Mirroring,Part079]
  Origin = -> Origin287
  Placement = pos=(-5.2,-45.6,200.6) rot=(1,0,0;1.5708rad)
FEATURE [App::Part] Part072  label="RL Leg"
  Group = -> [Part096,Part099,Part068]
  Origin = -> Origin249
  Placement = pos=(-206,0,0) rot=(0,0,1;0rad)
FEATURE [Sketcher::SketchObject] Sketch1103
  MapMode = 5
  Placement = pos=(0,0,0) rot=(1,0,0;1.5708rad)
  Support = -> [XZ_Plane401]
  sketch-geometry (8):
    g0: LineSegment StartX=-1.5 StartY=2.25 StartZ=0 EndX=-3.25 EndY=2.25 EndZ=0
    g1: LineSegment StartX=-3.25 StartY=2.25 StartZ=0 EndX=-3.25 EndY=1.25 EndZ=0
    g2: LineSegment StartX=-3.25 StartY=1.25 StartZ=0 EndX=-2 EndY=1.25 EndZ=0
    g3: LineSegment StartX=-2 StartY=1.25 StartZ=0 EndX=-2 EndY=-1.25 EndZ=0
    g4: LineSegment StartX=-2 StartY=-1.25 StartZ=0 EndX=-3.25 EndY=-1.25 EndZ=0
    g5: LineSegment StartX=-3.25 StartY=-1.25 StartZ=0 EndX=-3.25 EndY=-2.25 EndZ=0
    g6: LineSegment StartX=-3.25 StartY=-2.25 StartZ=0 EndX=-1.5 EndY=-2.25 EndZ=0
    g7: LineSegment StartX=-1.5 StartY=-2.25 StartZ=0 EndX=-1.5 EndY=2.25 EndZ=0
  constraints (23):
    c: Horizontal(g0)
    c: Coincident(g0,g1)
    c: Vertical(g1)
    c: Coincident(g1,g2)
    c: Horizontal(g2)
    c: Coincident(g2,g3)
    c: Vertical(g3)
    c: Coincident(g3,g4)
    c: Horizontal(g4)
    c: Coincident(g4,g5)
    c: Vertical(g5)
    c: Coincident(g5,g6)
    c: Horizontal(g6)
    c: Coincident(g6,g7)
    c: Vertical(g7)
    c: Coincident(g0,g7)
    c: Equal(g1,g5)
    c: Symmetric(g4,g1,g-1)
    c: DistanceX(g0,g-1) = 1.5
    c: DistanceY(g3,g3) = 2.5
    c: DistanceY(g7,g7) = 4.5
    c: DistanceX(g0,g-1) = 3.25
    c: DistanceX(g2,g-1) = 2
FEATURE [PartDesign::Revolution] Revolution015
  Angle = 360
  Axis = (0,2e-16,1)
  Base = (0,0,0)
  Placement = pos=(0,0,0) rot=(1,0,0;1.5708rad)
  Profile = -> Sketch1103
  ReferenceAxis = -> Sketch1103 [V_Axis]
FEATURE [PartDesign::Fillet] Fillet137
  Base = -> Revolution015 [Face2,Face6,Edge1,Edge11,Face4]
  BaseFeature = -> Revolution015
  Placement = pos=(0,0,0) rot=(1,0,0;1.5708rad)
  Radius = 0.25
FEATURE [PartDesign::Body] Body284  label="Rubber Dampener013"
  Group = -> [Sketch1103,Revolution015,Fillet137]
  Origin = -> Origin397
  Placement = pos=(-62.3,-12.25,93.7) rot=(-1,0,0;1.5708rad)
  Tip = -> Fillet137
FEATURE [Sketcher::SketchObject] Sketch1104
  MapMode = 5
  Placement = pos=(0,0,0) rot=(1,0,0;1.5708rad)
  Support = -> [XZ_Plane400]
  sketch-geometry (8):
    g0: LineSegment StartX=-1.5 StartY=2.25 StartZ=0 EndX=-3.25 EndY=2.25 EndZ=0
    g1: LineSegment StartX=-3.25 StartY=2.25 StartZ=0 EndX=-3.25 EndY=1.25 EndZ=0
    g2: LineSegment StartX=-3.25 StartY=1.25 StartZ=0 EndX=-2 EndY=1.25 EndZ=0
    g3: LineSegment StartX=-2 StartY=1.25 StartZ=0 EndX=-2 EndY=-1.25 EndZ=0
    g4: LineSegment StartX=-2 StartY=-1.25 StartZ=0 EndX=-3.25 EndY=-1.25 EndZ=0
    g5: LineSegment StartX=-3.25 StartY=-1.25 StartZ=0 EndX=-3.25 EndY=-2.25 EndZ=0
    g6: LineSegment StartX=-3.25 StartY=-2.25 StartZ=0 EndX=-1.5 EndY=-2.25 EndZ=0
    g7: LineSegment StartX=-1.5 StartY=-2.25 StartZ=0 EndX=-1.5 EndY=2.25 EndZ=0
  constraints (23):
    c: Horizontal(g0)
    c: Coincident(g0,g1)
    c: Vertical(g1)
    c: Coincident(g1,g2)
    c: Horizontal(g2)
    c: Coincident(g2,g3)
    c: Vertical(g3)
    c: Coincident(g3,g4)
    c: Horizontal(g4)
    c: Coincident(g4,g5)
    c: Vertical(g5)
    c: Coincident(g5,g6)
    c: Horizontal(g6)
    c: Coincident(g6,g7)
    c: Vertical(g7)
    c: Coincident(g0,g7)
    c: Equal(g1,g5)
    c: Symmetric(g4,g1,g-1)
    c: DistanceX(g0,g-1) = 1.5
    c: DistanceY(g3,g3) = 2.5
    c: DistanceY(g7,g7) = 4.5
    c: DistanceX(g0,g-1) = 3.25
    c: DistanceX(g2,g-1) = 2
FEATURE [PartDesign::Revolution] Revolution013
  Angle = 360
  Axis = (0,2e-16,1)
  Base = (0,0,0)
  Placement = pos=(0,0,0) rot=(1,0,0;1.5708rad)
  Profile = -> Sketch1104
  ReferenceAxis = -> Sketch1104 [V_Axis]
FEATURE [PartDesign::Fillet] Fillet134
  Base = -> Revolution013 [Face2,Face6,Edge1,Edge11,Face4]
  BaseFeature = -> Revolution013
  Placement = pos=(0,0,0) rot=(1,0,0;1.5708rad)
  Radius = 0.25
FEATURE [PartDesign::Body] Body283  label="Rubber Dampener012"
  Group = -> [Sketch1104,Revolution013,Fillet134]
  Origin = -> Origin399
  Placement = pos=(-55.25,-12.25,100.75) rot=(-1,0,0;1.5708rad)
  Tip = -> Fillet134
FEATURE [Sketcher::SketchObject] Sketch1105
  MapMode = 5
  Placement = pos=(0,0,0) rot=(1,0,0;1.5708rad)
  Support = -> [XZ_Plane399]
  sketch-geometry (8):
    g0: LineSegment StartX=-1.5 StartY=2.25 StartZ=0 EndX=-3.25 EndY=2.25 EndZ=0
    g1: LineSegment StartX=-3.25 StartY=2.25 StartZ=0 EndX=-3.25 EndY=1.25 EndZ=0
    g2: LineSegment StartX=-3.25 StartY=1.25 StartZ=0 EndX=-2 EndY=1.25 EndZ=0
    g3: LineSegment StartX=-2 StartY=1.25 StartZ=0 EndX=-2 EndY=-1.25 EndZ=0
    g4: LineSegment StartX=-2 StartY=-1.25 StartZ=0 EndX=-3.25 EndY=-1.25 EndZ=0
    g5: LineSegment StartX=-3.25 StartY=-1.25 StartZ=0 EndX=-3.25 EndY=-2.25 EndZ=0
    g6: LineSegment StartX=-3.25 StartY=-2.25 StartZ=0 EndX=-1.5 EndY=-2.25 EndZ=0
    g7: LineSegment StartX=-1.5 StartY=-2.25 StartZ=0 EndX=-1.5 EndY=2.25 EndZ=0
  constraints (23):
    c: Horizontal(g0)
    c: Coincident(g0,g1)
    c: Vertical(g1)
    c: Coincident(g1,g2)
    c: Horizontal(g2)
    c: Coincident(g2,g3)
    c: Vertical(g3)
    c: Coincident(g3,g4)
    c: Horizontal(g4)
    c: Coincident(g4,g5)
    c: Vertical(g5)
    c: Coincident(g5,g6)
    c: Horizontal(g6)
    c: Coincident(g6,g7)
    c: Vertical(g7)
    c: Coincident(g0,g7)
    c: Equal(g1,g5)
    c: Symmetric(g4,g1,g-1)
    c: DistanceX(g0,g-1) = 1.5
    c: DistanceY(g3,g3) = 2.5
    c: DistanceY(g7,g7) = 4.5
    c: DistanceX(g0,g-1) = 3.25
    c: DistanceX(g2,g-1) = 2
FEATURE [PartDesign::Revolution] Revolution012
  Angle = 360
  Axis = (0,2e-16,1)
  Base = (0,0,0)
  Placement = pos=(0,0,0) rot=(1,0,0;1.5708rad)
  Profile = -> Sketch1105
  ReferenceAxis = -> Sketch1105 [V_Axis]
FEATURE [PartDesign::Fillet] Fillet136
  Base = -> Revolution012 [Face2,Face6,Edge1,Edge11,Face4]
  BaseFeature = -> Revolution012
  Placement = pos=(0,0,0) rot=(1,0,0;1.5708rad)
  Radius = 0.25
FEATURE [PartDesign::Body] Body286  label="Rubber Dampener015"
  Group = -> [Sketch1105,Revolution012,Fillet136]
  Origin = -> Origin398
  Placement = pos=(-96.5,-12.25,127.7) rot=(-1,0,0;1.5708rad)
  Tip = -> Fillet136
FEATURE [Sketcher::SketchObject] Sketch1106
  MapMode = 5
  Placement = pos=(0,0,0) rot=(1,0,0;1.5708rad)
  Support = -> [XZ_Plane397]
  sketch-geometry (8):
    g0: LineSegment StartX=-1.5 StartY=2.25 StartZ=0 EndX=-3.25 EndY=2.25 EndZ=0
    g1: LineSegment StartX=-3.25 StartY=2.25 StartZ=0 EndX=-3.25 EndY=1.25 EndZ=0
    g2: LineSegment StartX=-3.25 StartY=1.25 StartZ=0 EndX=-2 EndY=1.25 EndZ=0
    g3: LineSegment StartX=-2 StartY=1.25 StartZ=0 EndX=-2 EndY=-1.25 EndZ=0
    g4: LineSegment StartX=-2 StartY=-1.25 StartZ=0 EndX=-3.25 EndY=-1.25 EndZ=0
    g5: LineSegment StartX=-3.25 StartY=-1.25 StartZ=0 EndX=-3.25 EndY=-2.25 EndZ=0
    g6: LineSegment StartX=-3.25 StartY=-2.25 StartZ=0 EndX=-1.5 EndY=-2.25 EndZ=0
    g7: LineSegment StartX=-1.5 StartY=-2.25 StartZ=0 EndX=-1.5 EndY=2.25 EndZ=0
  constraints (23):
    c: Horizontal(g0)
    c: Coincident(g0,g1)
    c: Vertical(g1)
    c: Coincident(g1,g2)
    c: Horizontal(g2)
    c: Coincident(g2,g3)
    c: Vertical(g3)
    c: Coincident(g3,g4)
    c: Horizontal(g4)
    c: Coincident(g4,g5)
    c: Vertical(g5)
    c: Coincident(g5,g6)
    c: Horizontal(g6)
    c: Coincident(g6,g7)
    c: Vertical(g7)
    c: Coincident(g0,g7)
    c: Equal(g1,g5)
    c: Symmetric(g4,g1,g-1)
    c: DistanceX(g0,g-1) = 1.5
    c: DistanceY(g3,g3) = 2.5
    c: DistanceY(g7,g7) = 4.5
    c: DistanceX(g0,g-1) = 3.25
    c: DistanceX(g2,g-1) = 2
FEATURE [PartDesign::Revolution] Revolution014
  Angle = 360
  Axis = (0,2e-16,1)
  Base = (0,0,0)
  Placement = pos=(0,0,0) rot=(1,0,0;1.5708rad)
  Profile = -> Sketch1106
  ReferenceAxis = -> Sketch1106 [V_Axis]
FEATURE [PartDesign::Fillet] Fillet135
  Base = -> Revolution014 [Face2,Face6,Edge1,Edge11,Face4]
  BaseFeature = -> Revolution014
  Placement = pos=(0,0,0) rot=(1,0,0;1.5708rad)
  Radius = 0.25
FEATURE [PartDesign::Body] Body285  label="Rubber Dampener014"
  Group = -> [Sketch1106,Revolution014,Fillet135]
  Origin = -> Origin400
  Placement = pos=(-89.5,-12.25,134.7) rot=(-1,0,0;1.5708rad)
  Tip = -> Fillet135
FEATURE [App::Part] Part111  label="Rubber Dampeners003"
  Group = -> [Body285,Body286,Body283,Body284]
  Origin = -> Origin401
  Placement = pos=(18.7923,-33.3866,66.0791) rot=(0.357407,0.357407,-0.862856;1.71777rad)
FEATURE [App::Part] Part065  label="FL Shoulder Joint Servo"
  Group = -> [Part064,Body159,Body160,Body161,Body162,Part066,Part111]
  Origin = -> Origin231
FEATURE [Sketcher::SketchObject] Sketch1107
  MapMode = 5
  Placement = pos=(0,0,0) rot=(1,0,0;1.5708rad)
  Support = -> [XZ_Plane406]
  sketch-geometry (8):
    g0: LineSegment StartX=-1.5 StartY=2.25 StartZ=0 EndX=-3.25 EndY=2.25 EndZ=0
    g1: LineSegment StartX=-3.25 StartY=2.25 StartZ=0 EndX=-3.25 EndY=1.25 EndZ=0
    g2: LineSegment StartX=-3.25 StartY=1.25 StartZ=0 EndX=-2 EndY=1.25 EndZ=0
    g3: LineSegment StartX=-2 StartY=1.25 StartZ=0 EndX=-2 EndY=-1.25 EndZ=0
    g4: LineSegment StartX=-2 StartY=-1.25 StartZ=0 EndX=-3.25 EndY=-1.25 EndZ=0
    g5: LineSegment StartX=-3.25 StartY=-1.25 StartZ=0 EndX=-3.25 EndY=-2.25 EndZ=0
    g6: LineSegment StartX=-3.25 StartY=-2.25 StartZ=0 EndX=-1.5 EndY=-2.25 EndZ=0
    g7: LineSegment StartX=-1.5 StartY=-2.25 StartZ=0 EndX=-1.5 EndY=2.25 EndZ=0
  constraints (23):
    c: Horizontal(g0)
    c: Coincident(g0,g1)
    c: Vertical(g1)
    c: Coincident(g1,g2)
    c: Horizontal(g2)
    c: Coincident(g2,g3)
    c: Vertical(g3)
    c: Coincident(g3,g4)
    c: Horizontal(g4)
    c: Coincident(g4,g5)
    c: Vertical(g5)
    c: Coincident(g5,g6)
    c: Horizontal(g6)
    c: Coincident(g6,g7)
    c: Vertical(g7)
    c: Coincident(g0,g7)
    c: Equal(g1,g5)
    c: Symmetric(g4,g1,g-1)
    c: DistanceX(g0,g-1) = 1.5
    c: DistanceY(g3,g3) = 2.5
    c: DistanceY(g7,g7) = 4.5
    c: DistanceX(g0,g-1) = 3.25
    c: DistanceX(g2,g-1) = 2
FEATURE [PartDesign::Revolution] Revolution016
  Angle = 360
  Axis = (0,2e-16,1)
  Base = (0,0,0)
  Placement = pos=(0,0,0) rot=(1,0,0;1.5708rad)
  Profile = -> Sketch1107
  ReferenceAxis = -> Sketch1107 [V_Axis]
FEATURE [PartDesign::Fillet] Fillet141
  Base = -> Revolution016 [Face2,Face6,Edge1,Edge11,Face4]
  BaseFeature = -> Revolution016
  Placement = pos=(0,0,0) rot=(1,0,0;1.5708rad)
  Radius = 0.25
FEATURE [PartDesign::Body] Body287  label="Rubber Dampener016"
  Group = -> [Sketch1107,Revolution016,Fillet141]
  Origin = -> Origin403
  Placement = pos=(-62.3,-12.25,93.7) rot=(-1,0,0;1.5708rad)
  Tip = -> Fillet141
FEATURE [Sketcher::SketchObject] Sketch1108
  MapMode = 5
  Placement = pos=(0,0,0) rot=(1,0,0;1.5708rad)
  Support = -> [XZ_Plane402]
  sketch-geometry (8):
    g0: LineSegment StartX=-1.5 StartY=2.25 StartZ=0 EndX=-3.25 EndY=2.25 EndZ=0
    g1: LineSegment StartX=-3.25 StartY=2.25 StartZ=0 EndX=-3.25 EndY=1.25 EndZ=0
    g2: LineSegment StartX=-3.25 StartY=1.25 StartZ=0 EndX=-2 EndY=1.25 EndZ=0
    g3: LineSegment StartX=-2 StartY=1.25 StartZ=0 EndX=-2 EndY=-1.25 EndZ=0
    g4: LineSegment StartX=-2 StartY=-1.25 StartZ=0 EndX=-3.25 EndY=-1.25 EndZ=0
    g5: LineSegment StartX=-3.25 StartY=-1.25 StartZ=0 EndX=-3.25 EndY=-2.25 EndZ=0
    g6: LineSegment StartX=-3.25 StartY=-2.25 StartZ=0 EndX=-1.5 EndY=-2.25 EndZ=0
    g7: LineSegment StartX=-1.5 StartY=-2.25 StartZ=0 EndX=-1.5 EndY=2.25 EndZ=0
  constraints (23):
    c: Horizontal(g0)
    c: Coincident(g0,g1)
    c: Vertical(g1)
    c: Coincident(g1,g2)
    c: Horizontal(g2)
    c: Coincident(g2,g3)
    c: Vertical(g3)
    c: Coincident(g3,g4)
    c: Horizontal(g4)
    c: Coincident(g4,g5)
    c: Vertical(g5)
    c: Coincident(g5,g6)
    c: Horizontal(g6)
    c: Coincident(g6,g7)
    c: Vertical(g7)
    c: Coincident(g0,g7)
    c: Equal(g1,g5)
    c: Symmetric(g4,g1,g-1)
    c: DistanceX(g0,g-1) = 1.5
    c: DistanceY(g3,g3) = 2.5
    c: DistanceY(g7,g7) = 4.5
    c: DistanceX(g0,g-1) = 3.25
    c: DistanceX(g2,g-1) = 2
FEATURE [PartDesign::Revolution] Revolution018
  Angle = 360
  Axis = (0,2e-16,1)
  Base = (0,0,0)
  Placement = pos=(0,0,0) rot=(1,0,0;1.5708rad)
  Profile = -> Sketch1108
  ReferenceAxis = -> Sketch1108 [V_Axis]
FEATURE [PartDesign::Fillet] Fillet139
  Base = -> Revolution018 [Face2,Face6,Edge1,Edge11,Face4]
  BaseFeature = -> Revolution018
  Placement = pos=(0,0,0) rot=(1,0,0;1.5708rad)
  Radius = 0.25
FEATURE [PartDesign::Body] Body288  label="Rubber Dampener017"
  Group = -> [Sketch1108,Revolution018,Fillet139]
  Origin = -> Origin402
  Placement = pos=(-96.5,-12.25,127.7) rot=(-1,0,0;1.5708rad)
  Tip = -> Fillet139
FEATURE [Sketcher::SketchObject] Sketch1109
  MapMode = 5
  Placement = pos=(0,0,0) rot=(1,0,0;1.5708rad)
  Support = -> [XZ_Plane405]
  sketch-geometry (8):
    g0: LineSegment StartX=-1.5 StartY=2.25 StartZ=0 EndX=-3.25 EndY=2.25 EndZ=0
    g1: LineSegment StartX=-3.25 StartY=2.25 StartZ=0 EndX=-3.25 EndY=1.25 EndZ=0
    g2: LineSegment StartX=-3.25 StartY=1.25 StartZ=0 EndX=-2 EndY=1.25 EndZ=0
    g3: LineSegment StartX=-2 StartY=1.25 StartZ=0 EndX=-2 EndY=-1.25 EndZ=0
    g4: LineSegment StartX=-2 StartY=-1.25 StartZ=0 EndX=-3.25 EndY=-1.25 EndZ=0
    g5: LineSegment StartX=-3.25 StartY=-1.25 StartZ=0 EndX=-3.25 EndY=-2.25 EndZ=0
    g6: LineSegment StartX=-3.25 StartY=-2.25 StartZ=0 EndX=-1.5 EndY=-2.25 EndZ=0
    g7: LineSegment StartX=-1.5 StartY=-2.25 StartZ=0 EndX=-1.5 EndY=2.25 EndZ=0
  constraints (23):
    c: Horizontal(g0)
    c: Coincident(g0,g1)
    c: Vertical(g1)
    c: Coincident(g1,g2)
    c: Horizontal(g2)
    c: Coincident(g2,g3)
    c: Vertical(g3)
    c: Coincident(g3,g4)
    c: Horizontal(g4)
    c: Coincident(g4,g5)
    c: Vertical(g5)
    c: Coincident(g5,g6)
    c: Horizontal(g6)
    c: Coincident(g6,g7)
    c: Vertical(g7)
    c: Coincident(g0,g7)
    c: Equal(g1,g5)
    c: Symmetric(g4,g1,g-1)
    c: DistanceX(g0,g-1) = 1.5
    c: DistanceY(g3,g3) = 2.5
    c: DistanceY(g7,g7) = 4.5
    c: DistanceX(g0,g-1) = 3.25
    c: DistanceX(g2,g-1) = 2
FEATURE [PartDesign::Revolution] Revolution017
  Angle = 360
  Axis = (0,2e-16,1)
  Base = (0,0,0)
  Placement = pos=(0,0,0) rot=(1,0,0;1.5708rad)
  Profile = -> Sketch1109
  ReferenceAxis = -> Sketch1109 [V_Axis]
FEATURE [PartDesign::Fillet] Fillet138
  Base = -> Revolution017 [Face2,Face6,Edge1,Edge11,Face4]
  BaseFeature = -> Revolution017
  Placement = pos=(0,0,0) rot=(1,0,0;1.5708rad)
  Radius = 0.25
FEATURE [PartDesign::Body] Body290  label="Rubber Dampener019"
  Group = -> [Sketch1109,Revolution017,Fillet138]
  Origin = -> Origin405
  Placement = pos=(-89.5,-12.25,134.7) rot=(-1,0,0;1.5708rad)
  Tip = -> Fillet138
FEATURE [Sketcher::SketchObject] Sketch1110
  MapMode = 5
  Placement = pos=(0,0,0) rot=(1,0,0;1.5708rad)
  Support = -> [XZ_Plane403]
  sketch-geometry (8):
    g0: LineSegment StartX=-1.5 StartY=2.25 StartZ=0 EndX=-3.25 EndY=2.25 EndZ=0
    g1: LineSegment StartX=-3.25 StartY=2.25 StartZ=0 EndX=-3.25 EndY=1.25 EndZ=0
    g2: LineSegment StartX=-3.25 StartY=1.25 StartZ=0 EndX=-2 EndY=1.25 EndZ=0
    g3: LineSegment StartX=-2 StartY=1.25 StartZ=0 EndX=-2 EndY=-1.25 EndZ=0
    g4: LineSegment StartX=-2 StartY=-1.25 StartZ=0 EndX=-3.25 EndY=-1.25 EndZ=0
    g5: LineSegment StartX=-3.25 StartY=-1.25 StartZ=0 EndX=-3.25 EndY=-2.25 EndZ=0
    g6: LineSegment StartX=-3.25 StartY=-2.25 StartZ=0 EndX=-1.5 EndY=-2.25 EndZ=0
    g7: LineSegment StartX=-1.5 StartY=-2.25 StartZ=0 EndX=-1.5 EndY=2.25 EndZ=0
  constraints (23):
    c: Horizontal(g0)
    c: Coincident(g0,g1)
    c: Vertical(g1)
    c: Coincident(g1,g2)
    c: Horizontal(g2)
    c: Coincident(g2,g3)
    c: Vertical(g3)
    c: Coincident(g3,g4)
    c: Horizontal(g4)
    c: Coincident(g4,g5)
    c: Vertical(g5)
    c: Coincident(g5,g6)
    c: Horizontal(g6)
    c: Coincident(g6,g7)
    c: Vertical(g7)
    c: Coincident(g0,g7)
    c: Equal(g1,g5)
    c: Symmetric(g4,g1,g-1)
    c: DistanceX(g0,g-1) = 1.5
    c: DistanceY(g3,g3) = 2.5
    c: DistanceY(g7,g7) = 4.5
    c: DistanceX(g0,g-1) = 3.25
    c: DistanceX(g2,g-1) = 2
FEATURE [PartDesign::Revolution] Revolution019
  Angle = 360
  Axis = (0,2e-16,1)
  Base = (0,0,0)
  Placement = pos=(0,0,0) rot=(1,0,0;1.5708rad)
  Profile = -> Sketch1110
  ReferenceAxis = -> Sketch1110 [V_Axis]
FEATURE [PartDesign::Fillet] Fillet140
  Base = -> Revolution019 [Face2,Face6,Edge1,Edge11,Face4]
  BaseFeature = -> Revolution019
  Placement = pos=(0,0,0) rot=(1,0,0;1.5708rad)
  Radius = 0.25
FEATURE [PartDesign::Body] Body289  label="Rubber Dampener018"
  Group = -> [Sketch1110,Revolution019,Fillet140]
  Origin = -> Origin404
  Placement = pos=(-55.25,-12.25,100.75) rot=(-1,0,0;1.5708rad)
  Tip = -> Fillet140
FEATURE [App::Part] Part112  label="Rubber Dampeners004"
  Group = -> [Body290,Body288,Body289,Body287]
  Origin = -> Origin406
FEATURE [App::Part] Part023  label="FL Lower Leg"
  Group = -> [Part025,Part026,Part002,Part003,Part004,Part024,Part112]
  Origin = -> Origin032
  Placement = pos=(-0.0178536,0,0.205627) rot=(0,0,1;0rad)
FEATURE [Sketcher::SketchObject] Sketch1111
  MapMode = 5
  Placement = pos=(0,0,0) rot=(1,0,0;1.5708rad)
  Support = -> [XZ_Plane407]
  sketch-geometry (8):
    g0: LineSegment StartX=-1.5 StartY=2.25 StartZ=0 EndX=-3.25 EndY=2.25 EndZ=0
    g1: LineSegment StartX=-3.25 StartY=2.25 StartZ=0 EndX=-3.25 EndY=1.25 EndZ=0
    g2: LineSegment StartX=-3.25 StartY=1.25 StartZ=0 EndX=-2 EndY=1.25 EndZ=0
    g3: LineSegment StartX=-2 StartY=1.25 StartZ=0 EndX=-2 EndY=-1.25 EndZ=0
    g4: LineSegment StartX=-2 StartY=-1.25 StartZ=0 EndX=-3.25 EndY=-1.25 EndZ=0
    g5: LineSegment StartX=-3.25 StartY=-1.25 StartZ=0 EndX=-3.25 EndY=-2.25 EndZ=0
    g6: LineSegment StartX=-3.25 StartY=-2.25 StartZ=0 EndX=-1.5 EndY=-2.25 EndZ=0
    g7: LineSegment StartX=-1.5 StartY=-2.25 StartZ=0 EndX=-1.5 EndY=2.25 EndZ=0
  constraints (23):
    c: Horizontal(g0)
    c: Coincident(g0,g1)
    c: Vertical(g1)
    c: Coincident(g1,g2)
    c: Horizontal(g2)
    c: Coincident(g2,g3)
    c: Vertical(g3)
    c: Coincident(g3,g4)
    c: Horizontal(g4)
    c: Coincident(g4,g5)
    c: Vertical(g5)
    c: Coincident(g5,g6)
    c: Horizontal(g6)
    c: Coincident(g6,g7)
    c: Vertical(g7)
    c: Coincident(g0,g7)
    c: Equal(g1,g5)
    c: Symmetric(g4,g1,g-1)
    c: DistanceX(g0,g-1) = 1.5
    c: DistanceY(g3,g3) = 2.5
    c: DistanceY(g7,g7) = 4.5
    c: DistanceX(g0,g-1) = 3.25
    c: DistanceX(g2,g-1) = 2
FEATURE [PartDesign::Revolution] Revolution020
  Angle = 360
  Axis = (0,2e-16,1)
  Base = (0,0,0)
  Placement = pos=(0,0,0) rot=(1,0,0;1.5708rad)
  Profile = -> Sketch1111
  ReferenceAxis = -> Sketch1111 [V_Axis]
FEATURE [PartDesign::Fillet] Fillet142
  Base = -> Revolution020 [Face2,Face6,Edge1,Edge11,Face4]
  BaseFeature = -> Revolution020
  Placement = pos=(0,0,0) rot=(1,0,0;1.5708rad)
  Radius = 0.25
FEATURE [PartDesign::Body] Body291  label="Rubber Dampener020"
  Group = -> [Sketch1111,Revolution020,Fillet142]
  Origin = -> Origin410
  Placement = pos=(-55.25,-12.25,100.75) rot=(-1,0,0;1.5708rad)
  Tip = -> Fillet142
FEATURE [Sketcher::SketchObject] Sketch1112
  MapMode = 5
  Placement = pos=(0,0,0) rot=(1,0,0;1.5708rad)
  Support = -> [XZ_Plane411]
  sketch-geometry (8):
    g0: LineSegment StartX=-1.5 StartY=2.25 StartZ=0 EndX=-3.25 EndY=2.25 EndZ=0
    g1: LineSegment StartX=-3.25 StartY=2.25 StartZ=0 EndX=-3.25 EndY=1.25 EndZ=0
    g2: LineSegment StartX=-3.25 StartY=1.25 StartZ=0 EndX=-2 EndY=1.25 EndZ=0
    g3: LineSegment StartX=-2 StartY=1.25 StartZ=0 EndX=-2 EndY=-1.25 EndZ=0
    g4: LineSegment StartX=-2 StartY=-1.25 StartZ=0 EndX=-3.25 EndY=-1.25 EndZ=0
    g5: LineSegment StartX=-3.25 StartY=-1.25 StartZ=0 EndX=-3.25 EndY=-2.25 EndZ=0
    g6: LineSegment StartX=-3.25 StartY=-2.25 StartZ=0 EndX=-1.5 EndY=-2.25 EndZ=0
    g7: LineSegment StartX=-1.5 StartY=-2.25 StartZ=0 EndX=-1.5 EndY=2.25 EndZ=0
  constraints (23):
    c: Horizontal(g0)
    c: Coincident(g0,g1)
    c: Vertical(g1)
    c: Coincident(g1,g2)
    c: Horizontal(g2)
    c: Coincident(g2,g3)
    c: Vertical(g3)
    c: Coincident(g3,g4)
    c: Horizontal(g4)
    c: Coincident(g4,g5)
    c: Vertical(g5)
    c: Coincident(g5,g6)
    c: Horizontal(g6)
    c: Coincident(g6,g7)
    c: Vertical(g7)
    c: Coincident(g0,g7)
    c: Equal(g1,g5)
    c: Symmetric(g4,g1,g-1)
    c: DistanceX(g0,g-1) = 1.5
    c: DistanceY(g3,g3) = 2.5
    c: DistanceY(g7,g7) = 4.5
    c: DistanceX(g0,g-1) = 3.25
    c: DistanceX(g2,g-1) = 2
FEATURE [PartDesign::Revolution] Revolution021
  Angle = 360
  Axis = (0,2e-16,1)
  Base = (0,0,0)
  Placement = pos=(0,0,0) rot=(1,0,0;1.5708rad)
  Profile = -> Sketch1112
  ReferenceAxis = -> Sketch1112 [V_Axis]
FEATURE [PartDesign::Fillet] Fillet143
  Base = -> Revolution021 [Face2,Face6,Edge1,Edge11,Face4]
  BaseFeature = -> Revolution021
  Placement = pos=(0,0,0) rot=(1,0,0;1.5708rad)
  Radius = 0.25
FEATURE [PartDesign::Body] Body294  label="Rubber Dampener023"
  Group = -> [Sketch1112,Revolution021,Fillet143]
  Origin = -> Origin411
  Placement = pos=(-62.3,-12.25,93.7) rot=(-1,0,0;1.5708rad)
  Tip = -> Fillet143
FEATURE [Sketcher::SketchObject] Sketch1113
  MapMode = 5
  Placement = pos=(0,0,0) rot=(1,0,0;1.5708rad)
  Support = -> [XZ_Plane410]
  sketch-geometry (8):
    g0: LineSegment StartX=-1.5 StartY=2.25 StartZ=0 EndX=-3.25 EndY=2.25 EndZ=0
    g1: LineSegment StartX=-3.25 StartY=2.25 StartZ=0 EndX=-3.25 EndY=1.25 EndZ=0
    g2: LineSegment StartX=-3.25 StartY=1.25 StartZ=0 EndX=-2 EndY=1.25 EndZ=0
    g3: LineSegment StartX=-2 StartY=1.25 StartZ=0 EndX=-2 EndY=-1.25 EndZ=0
    g4: LineSegment StartX=-2 StartY=-1.25 StartZ=0 EndX=-3.25 EndY=-1.25 EndZ=0
    g5: LineSegment StartX=-3.25 StartY=-1.25 StartZ=0 EndX=-3.25 EndY=-2.25 EndZ=0
    g6: LineSegment StartX=-3.25 StartY=-2.25 StartZ=0 EndX=-1.5 EndY=-2.25 EndZ=0
    g7: LineSegment StartX=-1.5 StartY=-2.25 StartZ=0 EndX=-1.5 EndY=2.25 EndZ=0
  constraints (23):
    c: Horizontal(g0)
    c: Coincident(g0,g1)
    c: Vertical(g1)
    c: Coincident(g1,g2)
    c: Horizontal(g2)
    c: Coincident(g2,g3)
    c: Vertical(g3)
    c: Coincident(g3,g4)
    c: Horizontal(g4)
    c: Coincident(g4,g5)
    c: Vertical(g5)
    c: Coincident(g5,g6)
    c: Horizontal(g6)
    c: Coincident(g6,g7)
    c: Vertical(g7)
    c: Coincident(g0,g7)
    c: Equal(g1,g5)
    c: Symmetric(g4,g1,g-1)
    c: DistanceX(g0,g-1) = 1.5
    c: DistanceY(g3,g3) = 2.5
    c: DistanceY(g7,g7) = 4.5
    c: DistanceX(g0,g-1) = 3.25
    c: DistanceX(g2,g-1) = 2
FEATURE [PartDesign::Revolution] Revolution023
  Angle = 360
  Axis = (0,2e-16,1)
  Base = (0,0,0)
  Placement = pos=(0,0,0) rot=(1,0,0;1.5708rad)
  Profile = -> Sketch1113
  ReferenceAxis = -> Sketch1113 [V_Axis]
FEATURE [PartDesign::Fillet] Fillet144
  Base = -> Revolution023 [Face2,Face6,Edge1,Edge11,Face4]
  BaseFeature = -> Revolution023
  Placement = pos=(0,0,0) rot=(1,0,0;1.5708rad)
  Radius = 0.25
FEATURE [PartDesign::Body] Body293  label="Rubber Dampener022"
  Group = -> [Sketch1113,Revolution023,Fillet144]
  Origin = -> Origin408
  Placement = pos=(-89.5,-12.25,134.7) rot=(-1,0,0;1.5708rad)
  Tip = -> Fillet144
FEATURE [Sketcher::SketchObject] Sketch1114
  MapMode = 5
  Placement = pos=(0,0,0) rot=(1,0,0;1.5708rad)
  Support = -> [XZ_Plane409]
  sketch-geometry (8):
    g0: LineSegment StartX=-1.5 StartY=2.25 StartZ=0 EndX=-3.25 EndY=2.25 EndZ=0
    g1: LineSegment StartX=-3.25 StartY=2.25 StartZ=0 EndX=-3.25 EndY=1.25 EndZ=0
    g2: LineSegment StartX=-3.25 StartY=1.25 StartZ=0 EndX=-2 EndY=1.25 EndZ=0
    g3: LineSegment StartX=-2 StartY=1.25 StartZ=0 EndX=-2 EndY=-1.25 EndZ=0
    g4: LineSegment StartX=-2 StartY=-1.25 StartZ=0 EndX=-3.25 EndY=-1.25 EndZ=0
    g5: LineSegment StartX=-3.25 StartY=-1.25 StartZ=0 EndX=-3.25 EndY=-2.25 EndZ=0
    g6: LineSegment StartX=-3.25 StartY=-2.25 StartZ=0 EndX=-1.5 EndY=-2.25 EndZ=0
    g7: LineSegment StartX=-1.5 StartY=-2.25 StartZ=0 EndX=-1.5 EndY=2.25 EndZ=0
  constraints (23):
    c: Horizontal(g0)
    c: Coincident(g0,g1)
    c: Vertical(g1)
    c: Coincident(g1,g2)
    c: Horizontal(g2)
    c: Coincident(g2,g3)
    c: Vertical(g3)
    c: Coincident(g3,g4)
    c: Horizontal(g4)
    c: Coincident(g4,g5)
    c: Vertical(g5)
    c: Coincident(g5,g6)
    c: Horizontal(g6)
    c: Coincident(g6,g7)
    c: Vertical(g7)
    c: Coincident(g0,g7)
    c: Equal(g1,g5)
    c: Symmetric(g4,g1,g-1)
    c: DistanceX(g0,g-1) = 1.5
    c: DistanceY(g3,g3) = 2.5
    c: DistanceY(g7,g7) = 4.5
    c: DistanceX(g0,g-1) = 3.25
    c: DistanceX(g2,g-1) = 2
FEATURE [PartDesign::Revolution] Revolution022
  Angle = 360
  Axis = (0,2e-16,1)
  Base = (0,0,0)
  Placement = pos=(0,0,0) rot=(1,0,0;1.5708rad)
  Profile = -> Sketch1114
  ReferenceAxis = -> Sketch1114 [V_Axis]
FEATURE [PartDesign::Fillet] Fillet145
  Base = -> Revolution022 [Face2,Face6,Edge1,Edge11,Face4]
  BaseFeature = -> Revolution022
  Placement = pos=(0,0,0) rot=(1,0,0;1.5708rad)
  Radius = 0.25
FEATURE [PartDesign::Body] Body292  label="Rubber Dampener021"
  Group = -> [Sketch1114,Revolution022,Fillet145]
  Origin = -> Origin407
  Placement = pos=(-96.5,-12.25,127.7) rot=(-1,0,0;1.5708rad)
  Tip = -> Fillet145
FEATURE [App::Part] Part113  label="Rubber Dampeners005"
  Group = -> [Body293,Body292,Body291,Body294]
  Origin = -> Origin409
  Placement = pos=(86.9205,-9.25,30.0402) rot=(0,-1,0;0.785398rad)
FEATURE [App::Part] Part027  label="FL Upper Leg"
  Group = -> [Part020,Part022,Body061,Body060,Part029,Part030,Part028,Part031,Part032,Part033,Body086,Part113]
  Origin = -> Origin093
  Placement = pos=(55.5497,0.15,169.885) rot=(0,1,0;5.75959rad)
FEATURE [App::Part] Part  label="FL Leg"
  Group = -> [Part023,Part027,Part052,Part065]
  Origin = -> Origin
FEATURE [PartDesign::Body] Body324
  Origin = -> Origin474
FEATURE [Sketcher::SketchObject] Sketch1116
  MapMode = 5
  Support = -> [XY_Plane554]
FEATURE [Sketcher::SketchObject] Sketch1117
  MapMode = 5
  Support = -> [XY_Plane568]
  sketch-geometry (64):
    g0: LineSegment [constr] StartX=-3.75 StartY=6.49519 StartZ=0 EndX=-7.5 EndY=0 EndZ=0
    g1: LineSegment [constr] StartX=-7.5 StartY=0 StartZ=0 EndX=-3.75 EndY=-6.49519 EndZ=0
    g2: LineSegment [constr] StartX=-3.75 StartY=-6.49519 StartZ=0 EndX=3.75 EndY=-6.49519 EndZ=0
    g3: LineSegment [constr] StartX=3.75 StartY=-6.49519 StartZ=0 EndX=7.5 EndY=0 EndZ=0
    g4: LineSegment [constr] StartX=7.5 StartY=0 StartZ=0 EndX=3.75 EndY=6.49519 EndZ=0
    g5: LineSegment [constr] StartX=3.75 StartY=6.49519 StartZ=0 EndX=-3.75 EndY=6.49519 EndZ=0
    g6: Circle [constr] CenterX=0 CenterY=0 CenterZ=0 NormalX=0 NormalY=0 NormalZ=1 AngleXU=0 Radius=7.5
    g7: LineSegment [constr] StartX=0 StartY=7.5 StartZ=0 EndX=-6.49519 EndY=3.75 EndZ=0
    g8: LineSegment [constr] StartX=-6.49519 StartY=3.75 StartZ=0 EndX=-6.49519 EndY=-3.75 EndZ=0
    g9: LineSegment [constr] StartX=-6.49519 StartY=-3.75 StartZ=0 EndX=9.8e-15 EndY=-7.5 EndZ=0
    g10: LineSegment [constr] StartX=9.8e-15 StartY=-7.5 StartZ=0 EndX=6.49519 EndY=-3.75 EndZ=0
    g11: LineSegment [constr] StartX=6.49519 StartY=-3.75 StartZ=0 EndX=6.49519 EndY=3.75 EndZ=0
    g12: LineSegment [constr] StartX=6.49519 StartY=3.75 StartZ=0 EndX=0 EndY=7.5 EndZ=0
    g13: Circle [constr] CenterX=0 CenterY=0 CenterZ=0 NormalX=0 NormalY=0 NormalZ=1 AngleXU=0 Radius=7.5
    g14: LineSegment [constr] StartX=0 StartY=10.5 StartZ=0 EndX=-9.09327 EndY=5.25 EndZ=0
    g15: LineSegment [constr] StartX=-9.09327 StartY=5.25 StartZ=0 EndX=-9.09327 EndY=-5.25 EndZ=0
    g16: LineSegment [constr] StartX=-9.09327 StartY=-5.25 StartZ=0 EndX=-1.42e-14 EndY=-10.5 EndZ=0
    g17: LineSegment [constr] StartX=-1.42e-14 StartY=-10.5 StartZ=0 EndX=9.09327 EndY=-5.25 EndZ=0
    g18: LineSegment [constr] StartX=9.09327 StartY=-5.25 StartZ=0 EndX=9.09327 EndY=5.25 EndZ=0
    g19: LineSegment [constr] StartX=9.09327 StartY=5.25 StartZ=0 EndX=0 EndY=10.5 EndZ=0
    g20: Circle [constr] CenterX=0 CenterY=0 CenterZ=0 NormalX=0 NormalY=0 NormalZ=1 AngleXU=0 Radius=10.5
    g21: LineSegment [constr] StartX=0 StartY=13.5 StartZ=0 EndX=-11.6913 EndY=6.75 EndZ=0
    g22: LineSegment [constr] StartX=-11.6913 StartY=6.75 StartZ=0 EndX=-11.6913 EndY=-6.75 EndZ=0
    g23: LineSegment [constr] StartX=-11.6913 StartY=-6.75 StartZ=0 EndX=0 EndY=-13.5 EndZ=0
    g24: LineSegment [constr] StartX=0 StartY=-13.5 StartZ=0 EndX=11.6913 EndY=-6.75 EndZ=0
    g25: LineSegment [constr] StartX=11.6913 StartY=-6.75 StartZ=0 EndX=11.6913 EndY=6.75 EndZ=0
    g26: LineSegment [constr] StartX=11.6913 StartY=6.75 StartZ=0 EndX=0 EndY=13.5 EndZ=0
    g27: Circle [constr] CenterX=0 CenterY=0 CenterZ=0 NormalX=0 NormalY=0 NormalZ=1 AngleXU=0 Radius=13.5
    g28: ArcOfCircle CenterX=0 CenterY=13.5 CenterZ=0 NormalX=0 NormalY=0 NormalZ=1 AngleXU=0 Radius=2.5 StartAngle=0.171439 EndAngle=2.97015
    g29: ArcOfCircle CenterX=11.6913 CenterY=6.75 CenterZ=0 NormalX=0 NormalY=0 NormalZ=1 AngleXU=0 Radius=2.5 StartAngle=5.40743 EndAngle=8.20614
    g30: ArcOfCircle CenterX=11.6913 CenterY=-6.75 CenterZ=0 NormalX=0 NormalY=0 NormalZ=1 AngleXU=0 Radius=2.5 StartAngle=4.36023 EndAngle=7.15894
    g31: ArcOfCircle CenterX=0 CenterY=-13.5 CenterZ=0 NormalX=0 NormalY=0 NormalZ=1 AngleXU=0 Radius=2.5 StartAngle=3.31303 EndAngle=6.11175
    g32: ArcOfCircle CenterX=-11.6913 CenterY=-6.75 CenterZ=0 NormalX=0 NormalY=0 NormalZ=1 AngleXU=0 Radius=2.5 StartAngle=2.26583 EndAngle=5.06455
    g33: ArcOfCircle CenterX=-11.6913 CenterY=6.75 CenterZ=0 NormalX=0 NormalY=0 NormalZ=1 AngleXU=0 Radius=2.5 StartAngle=1.21864 EndAngle=4.01735
    g34: LineSegment StartX=-10.829 StartY=9.09658 StartZ=0 EndX=-3.75 EndY=6.49519 EndZ=0
    g35: LineSegment StartX=-3.75 StartY=6.49519 StartZ=0 EndX=-2.46335 EndY=13.9265 EndZ=0
    g36: LineSegment StartX=2.46335 StartY=13.9265 StartZ=0 EndX=3.75 EndY=6.49519 EndZ=0
    g37: LineSegment StartX=3.75 StartY=6.49519 StartZ=0 EndX=10.829 EndY=9.09658 EndZ=0
    g38: LineSegment StartX=13.2924 StartY=4.82993 StartZ=0 EndX=7.5 EndY=0 EndZ=0
    g39: LineSegment StartX=7.5 StartY=0 StartZ=0 EndX=13.2924 EndY=-4.82993 EndZ=0
    g40: LineSegment StartX=10.829 StartY=-9.09658 StartZ=0 EndX=3.75 EndY=-6.49519 EndZ=0
    g41: LineSegment StartX=3.75 StartY=-6.49519 StartZ=0 EndX=2.46335 EndY=-13.9265 EndZ=0
    g42: LineSegment StartX=-2.46335 StartY=-13.9265 StartZ=0 EndX=-3.75 EndY=-6.49519 EndZ=0
    g43: LineSegment StartX=-3.75 StartY=-6.49519 StartZ=0 EndX=-10.829 EndY=-9.09658 EndZ=0
    g44: LineSegment StartX=-13.2924 StartY=-4.82993 StartZ=0 EndX=-7.5 EndY=0 EndZ=0
    g45: LineSegment StartX=-7.5 StartY=0 StartZ=0 EndX=-13.2924 EndY=4.82993 EndZ=0
    g46: Circle CenterX=-11.6913 CenterY=6.75 CenterZ=0 NormalX=0 NormalY=0 NormalZ=1 AngleXU=0 Radius=0.75
    g47: Circle CenterX=-9.09327 CenterY=5.25 CenterZ=0 NormalX=0 NormalY=0 NormalZ=1 AngleXU=0 Radius=0.75
    g48: Circle CenterX=-6.49519 CenterY=3.75 CenterZ=0 NormalX=0 NormalY=0 NormalZ=1 AngleXU=0 Radius=0.75
    g49: Circle CenterX=0 CenterY=13.5 CenterZ=0 NormalX=0 NormalY=0 NormalZ=1 AngleXU=0 Radius=0.75
    g50: Circle CenterX=0 CenterY=10.5 CenterZ=0 NormalX=0 NormalY=0 NormalZ=1 AngleXU=0 Radius=0.75
    g51: Circle CenterX=0 CenterY=7.5 CenterZ=0 NormalX=0 NormalY=0 NormalZ=1 AngleXU=0 Radius=0.75
    g52: Circle CenterX=11.6913 CenterY=6.75 CenterZ=0 NormalX=0 NormalY=0 NormalZ=1 AngleXU=0 Radius=0.75
    g53: Circle CenterX=9.09327 CenterY=5.25 CenterZ=0 NormalX=0 NormalY=0 NormalZ=1 AngleXU=0 Radius=0.75
    g54: Circle CenterX=6.49519 CenterY=3.75 CenterZ=0 NormalX=0 NormalY=0 NormalZ=1 AngleXU=0 Radius=0.75
    g55: Circle CenterX=11.6913 CenterY=-6.75 CenterZ=0 NormalX=0 NormalY=0 NormalZ=1 AngleXU=0 Radius=0.75
    g56: Circle CenterX=9.09327 CenterY=-5.25 CenterZ=0 NormalX=0 NormalY=0 NormalZ=1 AngleXU=0 Radius=0.75
    g57: Circle CenterX=6.49519 CenterY=-3.75 CenterZ=0 NormalX=0 NormalY=0 NormalZ=1 AngleXU=0 Radius=0.75
    g58: Circle CenterX=9.8e-15 CenterY=-7.5 CenterZ=0 NormalX=0 NormalY=0 NormalZ=1 AngleXU=0 Radius=0.75
    g59: Circle CenterX=-1.42e-14 CenterY=-10.5 CenterZ=0 NormalX=0 NormalY=0 NormalZ=1 AngleXU=0 Radius=0.75
    g60: Circle CenterX=0 CenterY=-13.5 CenterZ=0 NormalX=0 NormalY=0 NormalZ=1 AngleXU=0 Radius=0.75
    g61: Circle CenterX=-11.6913 CenterY=-6.75 CenterZ=0 NormalX=0 NormalY=0 NormalZ=1 AngleXU=0 Radius=0.75
    g62: Circle CenterX=-9.09327 CenterY=-5.25 CenterZ=0 NormalX=0 NormalY=0 NormalZ=1 AngleXU=0 Radius=0.75
    g63: Circle CenterX=-6.49519 CenterY=-3.75 CenterZ=0 NormalX=0 NormalY=0 NormalZ=1 AngleXU=0 Radius=0.75
  constraints (136):
    c: Coincident(g0,g1)
    c: Coincident(g1,g2)
    c: Coincident(g2,g3)
    c: Coincident(g3,g4)
    c: Coincident(g4,g5)
    c: Coincident(g5,g0)
    c: Equal(g0, g1-g5) x5
    c: PointOnObject(g0,g6)
    c: PointOnObject(g1,g6)
    c: PointOnObject(g2,g6)
    c: PointOnObject(g3,g6)
    c: PointOnObject(g4,g6)
    c: PointOnObject(g5,g6)
    c: Coincident(g6,g-1)
    c: Coincident(g7,g8)
    c: Coincident(g8,g9)
    c: Coincident(g9,g10)
    c: Coincident(g10,g11)
    c: Coincident(g11,g12)
    c: Coincident(g12,g7)
    c: Equal(g7, g8-g12) x5
    c: PointOnObject(g7,g13)
    c: PointOnObject(g8,g13)
    c: PointOnObject(g9,g13)
    c: PointOnObject(g10,g13)
    c: PointOnObject(g11,g13)
    c: PointOnObject(g12,g13)
    c: Coincident(g13,g-1)
    c: PointOnObject(g12,g6)
    c: PointOnObject(g7,g-2)
    c: Horizontal(g5)
    c: Radius(g6) = 7.5
    c: Coincident(g14,g15)
    c: Coincident(g15,g16)
    c: Coincident(g16,g17)
    c: Coincident(g17,g18)
    c: Coincident(g18,g19)
    c: Coincident(g19,g14)
    c: Equal(g14, g15-g19) x5
    c: PointOnObject(g14,g20)
    c: PointOnObject(g15,g20)
    c: PointOnObject(g16,g20)
    c: PointOnObject(g17,g20)
    c: PointOnObject(g18,g20)
    c: PointOnObject(g19,g20)
    c: Coincident(g20,g-1)
    c: PointOnObject(g19,g-2)
    c: Radius(g20) = 10.5
    c: Coincident(g21,g22)
    c: Coincident(g22,g23)
    c: Coincident(g23,g24)
    c: Coincident(g24,g25)
    c: Coincident(g25,g26)
    c: Coincident(g26,g21)
    c: Equal(g21, g22-g26) x5
    c: PointOnObject(g21,g27)
    c: PointOnObject(g22,g27)
    c: PointOnObject(g23,g27)
    c: PointOnObject(g24,g27)
    c: PointOnObject(g25,g27)
    c: PointOnObject(g26,g27)
    c: Coincident(g27,g-1)
    c: PointOnObject(g26,g-2)
    c: Radius(g27) = 13.5
    c: Coincident(g28,g21)
    c: Coincident(g29,g25)
    c: Coincident(g30,g24)
    c: Coincident(g31,g23)
    c: Coincident(g32,g22)
    c: Coincident(g33,g21)
    c: Coincident(g34,g0)
    c: Coincident(g35,g34)
    c: Coincident(g36,g4)
    c: Coincident(g37,g36)
    c: Coincident(g38,g3)
    c: Coincident(g39,g38)
    c: Coincident(g40,g2)
    c: Coincident(g41,g40)
    c: Coincident(g42,g1)
    c: Coincident(g43,g42)
    c: Coincident(g44,g0)
    c: Coincident(g45,g44)
    c: Tangent(g35,g28) = 1.5708
    c: Tangent(g36,g28) = 1.5708
    c: Tangent(g37,g29) = 1.5708
    c: Tangent(g38,g29) = 1.5708
    c: Tangent(g39,g30) = 1.5708
    c: Tangent(g40,g30) = 1.5708
    c: Tangent(g41,g31) = 1.5708
    c: Tangent(g42,g31) = 1.5708
    c: Tangent(g43,g32) = 1.5708
    c: Tangent(g44,g32) = 1.5708
    c: Tangent(g45,g33) = 1.5708
    c: Tangent(g34,g33) = 1.5708
    c: Radius(g29) = 2.5
    c: Equal(g29,g28)
    c: Equal(g28,g33)
    c: Equal(g33,g32)
    c: Equal(g32,g31)
    c: Equal(g31,g30)
    c: Coincident(g46,g33)
    c: Coincident(g47,g14)
    c: Coincident(g48,g7)
    c: Coincident(g49,g28)
    c: Coincident(g50,g14)
    c: Coincident(g51,g7)
    c: Coincident(g52,g29)
    c: Coincident(g53,g18)
    c: Coincident(g54,g11)
    c: Coincident(g55,g30)
    c: Coincident(g56,g17)
    c: Coincident(g57,g10)
    c: Coincident(g58,g9)
    c: Coincident(g59,g16)
    c: Coincident(g60,g31)
    c: Coincident(g61,g32)
    c: Coincident(g62,g15)
    c: Coincident(g63,g8)
    c: Equal(g61,g62)
    c: Equal(g62,g63)
    c: Equal(g63,g58)
    c: Equal(g58,g59)
    c: Equal(g59,g60)
    c: Equal(g60,g55)
    c: Equal(g55,g56)
    c: Equal(g56,g57)
    c: Equal(g57,g54)
    c: Equal(g54,g53)
    c: Equal(g53,g52)
    c: Equal(g52,g51)
    c: Equal(g51,g50)
    c: Equal(g50,g49)
    c: Equal(g49,g46)
    c: Equal(g46,g47)
    c: Equal(g47,g48)
    c: Radius(g55) = 0.75
FEATURE [Sketcher::SketchObject] Sketch1118
  MapMode = 5
  Support = -> [XY_Plane554]
FEATURE [Sketcher::SketchObject] Sketch1121
  MapMode = 5
  Placement = pos=(0,0,0) rot=(1,0,0;1.5708rad)
  Support = -> [XZ_Plane459]
  sketch-geometry (8):
    g0: LineSegment StartX=-1.5 StartY=2.25 StartZ=0 EndX=-3.25 EndY=2.25 EndZ=0
    g1: LineSegment StartX=-3.25 StartY=2.25 StartZ=0 EndX=-3.25 EndY=1.25 EndZ=0
    g2: LineSegment StartX=-3.25 StartY=1.25 StartZ=0 EndX=-2 EndY=1.25 EndZ=0
    g3: LineSegment StartX=-2 StartY=1.25 StartZ=0 EndX=-2 EndY=-1.25 EndZ=0
    g4: LineSegment StartX=-2 StartY=-1.25 StartZ=0 EndX=-3.25 EndY=-1.25 EndZ=0
    g5: LineSegment StartX=-3.25 StartY=-1.25 StartZ=0 EndX=-3.25 EndY=-2.25 EndZ=0
    g6: LineSegment StartX=-3.25 StartY=-2.25 StartZ=0 EndX=-1.5 EndY=-2.25 EndZ=0
    g7: LineSegment StartX=-1.5 StartY=-2.25 StartZ=0 EndX=-1.5 EndY=2.25 EndZ=0
  constraints (23):
    c: Horizontal(g0)
    c: Coincident(g0,g1)
    c: Vertical(g1)
    c: Coincident(g1,g2)
    c: Horizontal(g2)
    c: Coincident(g2,g3)
    c: Vertical(g3)
    c: Coincident(g3,g4)
    c: Horizontal(g4)
    c: Coincident(g4,g5)
    c: Vertical(g5)
    c: Coincident(g5,g6)
    c: Horizontal(g6)
    c: Coincident(g6,g7)
    c: Vertical(g7)
    c: Coincident(g0,g7)
    c: Equal(g1,g5)
    c: Symmetric(g4,g1,g-1)
    c: DistanceX(g0,g-1) = 1.5
    c: DistanceY(g3,g3) = 2.5
    c: DistanceY(g7,g7) = 4.5
    c: DistanceX(g0,g-1) = 3.25
    c: DistanceX(g2,g-1) = 2
FEATURE [Sketcher::SketchObject] Sketch1130
  MapMode = 5
  Support = -> [XY_Plane566]
  sketch-geometry (9):
    g0: ArcOfCircle CenterX=0 CenterY=0 CenterZ=0 NormalX=0 NormalY=0 NormalZ=1 AngleXU=0 Radius=16.5 StartAngle=2.61799 EndAngle=5.75959
    g1: LineSegment StartX=-14.2894 StartY=8.25 StartZ=0 EndX=-1.3577 EndY=30.6484 EndZ=0
    g2: ArcOfCircle CenterX=23.5 CenterY=16.2968 CenterZ=0 NormalX=0 NormalY=0 NormalZ=1 AngleXU=0 Radius=28.7032 StartAngle=1.5708 EndAngle=2.61799
    g3: LineSegment StartX=23.5 StartY=45 StartZ=0 EndX=40 EndY=45 EndZ=0
    g4: LineSegment StartX=40 StartY=45 StartZ=0 EndX=40 EndY=15 EndZ=0
    g5: LineSegment StartX=40 StartY=15 StartZ=0 EndX=28.6962 EndY=15 EndZ=0
    g6: ArcOfCircle CenterX=28.6962 CenterY=13.2968 CenterZ=0 NormalX=0 NormalY=0 NormalZ=1 AngleXU=0 Radius=1.70319 StartAngle=1.5708 EndAngle=2.61799
    g7: LineSegment StartX=27.2211 StartY=14.1484 StartZ=0 EndX=14.2894 EndY=-8.25 EndZ=0
    g8: LineSegment [constr] StartX=-1.3577 StartY=30.6484 StartZ=0 EndX=27.2211 EndY=14.1484 EndZ=0
  constraints (21):
    c: Tangent(g0,g1) = 1.5708
    c: Tangent(g1,g2) = 1.5708
    c: Tangent(g2,g3) = 1.5708
    c: Perpendicular(g3,g4) = 4.71239
    c: Coincident(g4,g5)
    c: Horizontal(g5)
    c: Tangent(g5,g6) = -1.5708
    c: Tangent(g6,g7) = -1.5708
    c: Parallel(g7,g1)
    c: Radius(g0) = 16.5
    c: Horizontal(g3)
    c: DistanceY(g4,g4) = 30
    c: Tangent(g7,g0) = 1.5708
    c: DistanceX(g0,g4) = 40
    c: Coincident(g8,g1)
    c: Coincident(g8,g6)
    c: Perpendicular(g1,g8)
    c: DistanceX(g3,g3) = 16.5
    c: DistanceY(g0,g4) = 15
    c: Angle(g8) = -0.523599
    c: Coincident(g0,g-1)
FEATURE [Sketcher::SketchObject] Sketch1131
  MapMode = 5
  Support = -> [XY_Plane554]
  sketch-geometry (8):
    g0: LineSegment StartX=0 StartY=2.3094 StartZ=0 EndX=-2 EndY=1.1547 EndZ=0
    g1: LineSegment StartX=-2 StartY=1.1547 StartZ=0 EndX=-2 EndY=-1.1547 EndZ=0
    g2: LineSegment StartX=-2 StartY=-1.1547 StartZ=0 EndX=-2e-16 EndY=-2.3094 EndZ=0
    g3: LineSegment StartX=-2e-16 StartY=-2.3094 StartZ=0 EndX=2 EndY=-1.1547 EndZ=0
    g4: LineSegment StartX=2 StartY=-1.1547 StartZ=0 EndX=2 EndY=1.1547 EndZ=0
    g5: LineSegment StartX=2 StartY=1.1547 StartZ=0 EndX=0 EndY=2.3094 EndZ=0
    g6: Circle [constr] CenterX=0 CenterY=0 CenterZ=0 NormalX=0 NormalY=0 NormalZ=1 AngleXU=0 Radius=2.3094
    g7: Circle CenterX=0 CenterY=0 CenterZ=0 NormalX=0 NormalY=0 NormalZ=1 AngleXU=0 Radius=1
  constraints (18):
    c: Coincident(g0,g1)
    c: Coincident(g1,g2)
    c: Coincident(g2,g3)
    c: Coincident(g3,g4)
    c: Coincident(g4,g5)
    c: Coincident(g5,g0)
    c: Equal(g0, g1-g5) x5
    c: PointOnObject(g0,g6)
    c: PointOnObject(g1,g6)
    c: PointOnObject(g2,g6)
    c: PointOnObject(g3,g6)
    c: PointOnObject(g4,g6)
    c: PointOnObject(g5,g6)
    c: Coincident(g6,g-1)
    c: PointOnObject(g5,g-2)
    c: DistanceX(g0,g4) = 4
    c: Coincident(g7,g-1)
    c: Radius(g7) = 1
FEATURE [Sketcher::SketchObject] Sketch1132
  MapMode = 5
  Support = -> [XY_Plane546]
  sketch-geometry (1):
    g0: Circle CenterX=0 CenterY=0 CenterZ=0 NormalX=0 NormalY=0 NormalZ=1 AngleXU=0 Radius=1.9
  constraints (2):
    c: Coincident(g0,g-1)
    c: Radius(g0) = 1.9
FEATURE [Sketcher::SketchObject] Sketch1133
  MapMode = 5
  Support = -> [XY_Plane571]
FEATURE [Sketcher::SketchObject] Sketch1136
  MapMode = 5
  Support = -> [XY_Plane569]
FEATURE [Sketcher::SketchObject] Sketch1137
  MapMode = 5
  Support = -> [XY_Plane569]
FEATURE [Sketcher::SketchObject] Sketch1141
  MapMode = 5
  Support = -> [XY_Plane571]
FEATURE [Sketcher::SketchObject] Sketch1142
  MapMode = 5
  Support = -> [XY_Plane559]
  sketch-geometry (8):
    g0: LineSegment StartX=0 StartY=2.3094 StartZ=0 EndX=-2 EndY=1.1547 EndZ=0
    g1: LineSegment StartX=-2 StartY=1.1547 StartZ=0 EndX=-2 EndY=-1.1547 EndZ=0
    g2: LineSegment StartX=-2 StartY=-1.1547 StartZ=0 EndX=-2e-16 EndY=-2.3094 EndZ=0
    g3: LineSegment StartX=-2e-16 StartY=-2.3094 StartZ=0 EndX=2 EndY=-1.1547 EndZ=0
    g4: LineSegment StartX=2 StartY=-1.1547 StartZ=0 EndX=2 EndY=1.1547 EndZ=0
    g5: LineSegment StartX=2 StartY=1.1547 StartZ=0 EndX=0 EndY=2.3094 EndZ=0
    g6: Circle [constr] CenterX=0 CenterY=0 CenterZ=0 NormalX=0 NormalY=0 NormalZ=1 AngleXU=0 Radius=2.3094
    g7: Circle CenterX=0 CenterY=0 CenterZ=0 NormalX=0 NormalY=0 NormalZ=1 AngleXU=0 Radius=1
  constraints (18):
    c: Coincident(g0,g1)
    c: Coincident(g1,g2)
    c: Coincident(g2,g3)
    c: Coincident(g3,g4)
    c: Coincident(g4,g5)
    c: Coincident(g5,g0)
    c: Equal(g0, g1-g5) x5
    c: PointOnObject(g0,g6)
    c: PointOnObject(g1,g6)
    c: PointOnObject(g2,g6)
    c: PointOnObject(g3,g6)
    c: PointOnObject(g4,g6)
    c: PointOnObject(g5,g6)
    c: Coincident(g6,g-1)
    c: PointOnObject(g5,g-2)
    c: DistanceX(g0,g4) = 4
    c: Coincident(g7,g-1)
    c: Radius(g7) = 1
FEATURE [Sketcher::SketchObject] Sketch1145
  MapMode = 5
  Support = -> [XY_Plane557]
FEATURE [Sketcher::SketchObject] Sketch1146
  MapMode = 5
  Support = -> [XY_Plane563]
  sketch-geometry (1):
    g0: Circle CenterX=0 CenterY=0 CenterZ=0 NormalX=0 NormalY=0 NormalZ=1 AngleXU=0 Radius=1.9
  constraints (2):
    c: Coincident(g0,g-1)
    c: Radius(g0) = 1.9
FEATURE [Sketcher::SketchObject] Sketch1148
  MapMode = 5
  Support = -> [XY_Plane543]
  sketch-geometry (8):
    g0: LineSegment StartX=0 StartY=2.3094 StartZ=0 EndX=-2 EndY=1.1547 EndZ=0
    g1: LineSegment StartX=-2 StartY=1.1547 StartZ=0 EndX=-2 EndY=-1.1547 EndZ=0
    g2: LineSegment StartX=-2 StartY=-1.1547 StartZ=0 EndX=-2e-16 EndY=-2.3094 EndZ=0
    g3: LineSegment StartX=-2e-16 StartY=-2.3094 StartZ=0 EndX=2 EndY=-1.1547 EndZ=0
    g4: LineSegment StartX=2 StartY=-1.1547 StartZ=0 EndX=2 EndY=1.1547 EndZ=0
    g5: LineSegment StartX=2 StartY=1.1547 StartZ=0 EndX=0 EndY=2.3094 EndZ=0
    g6: Circle [constr] CenterX=0 CenterY=0 CenterZ=0 NormalX=0 NormalY=0 NormalZ=1 AngleXU=0 Radius=2.3094
    g7: Circle CenterX=0 CenterY=0 CenterZ=0 NormalX=0 NormalY=0 NormalZ=1 AngleXU=0 Radius=1
  constraints (18):
    c: Coincident(g0,g1)
    c: Coincident(g1,g2)
    c: Coincident(g2,g3)
    c: Coincident(g3,g4)
    c: Coincident(g4,g5)
    c: Coincident(g5,g0)
    c: Equal(g0, g1-g5) x5
    c: PointOnObject(g0,g6)
    c: PointOnObject(g1,g6)
    c: PointOnObject(g2,g6)
    c: PointOnObject(g3,g6)
    c: PointOnObject(g4,g6)
    c: PointOnObject(g5,g6)
    c: Coincident(g6,g-1)
    c: PointOnObject(g5,g-2)
    c: DistanceX(g0,g4) = 4
    c: Coincident(g7,g-1)
    c: Radius(g7) = 1
FEATURE [Sketcher::SketchObject] Sketch1149
  MapMode = 5
  Support = -> [XY_Plane547]
  sketch-geometry (1):
    g0: Circle CenterX=0 CenterY=0 CenterZ=0 NormalX=0 NormalY=0 NormalZ=1 AngleXU=0 Radius=1.9
  constraints (2):
    c: Coincident(g0,g-1)
    c: Radius(g0) = 1.9
FEATURE [Sketcher::SketchObject] Sketch1151
  MapMode = 5
  Support = -> [XY_Plane571]
  sketch-geometry (8):
    g0: LineSegment StartX=0 StartY=2.3094 StartZ=0 EndX=-2 EndY=1.1547 EndZ=0
    g1: LineSegment StartX=-2 StartY=1.1547 StartZ=0 EndX=-2 EndY=-1.1547 EndZ=0
    g2: LineSegment StartX=-2 StartY=-1.1547 StartZ=0 EndX=-2e-16 EndY=-2.3094 EndZ=0
    g3: LineSegment StartX=-2e-16 StartY=-2.3094 StartZ=0 EndX=2 EndY=-1.1547 EndZ=0
    g4: LineSegment StartX=2 StartY=-1.1547 StartZ=0 EndX=2 EndY=1.1547 EndZ=0
    g5: LineSegment StartX=2 StartY=1.1547 StartZ=0 EndX=0 EndY=2.3094 EndZ=0
    g6: Circle [constr] CenterX=0 CenterY=0 CenterZ=0 NormalX=0 NormalY=0 NormalZ=1 AngleXU=0 Radius=2.3094
    g7: Circle CenterX=0 CenterY=0 CenterZ=0 NormalX=0 NormalY=0 NormalZ=1 AngleXU=0 Radius=1
  constraints (18):
    c: Coincident(g0,g1)
    c: Coincident(g1,g2)
    c: Coincident(g2,g3)
    c: Coincident(g3,g4)
    c: Coincident(g4,g5)
    c: Coincident(g5,g0)
    c: Equal(g0, g1-g5) x5
    c: PointOnObject(g0,g6)
    c: PointOnObject(g1,g6)
    c: PointOnObject(g2,g6)
    c: PointOnObject(g3,g6)
    c: PointOnObject(g4,g6)
    c: PointOnObject(g5,g6)
    c: Coincident(g6,g-1)
    c: PointOnObject(g5,g-2)
    c: DistanceX(g0,g4) = 4
    c: Coincident(g7,g-1)
    c: Radius(g7) = 1
FEATURE [Sketcher::SketchObject] Sketch1154
  MapMode = 5
  Support = -> [XY_Plane557]
  sketch-geometry (8):
    g0: LineSegment StartX=0 StartY=2.3094 StartZ=0 EndX=-2 EndY=1.1547 EndZ=0
    g1: LineSegment StartX=-2 StartY=1.1547 StartZ=0 EndX=-2 EndY=-1.1547 EndZ=0
    g2: LineSegment StartX=-2 StartY=-1.1547 StartZ=0 EndX=-2e-16 EndY=-2.3094 EndZ=0
    g3: LineSegment StartX=-2e-16 StartY=-2.3094 StartZ=0 EndX=2 EndY=-1.1547 EndZ=0
    g4: LineSegment StartX=2 StartY=-1.1547 StartZ=0 EndX=2 EndY=1.1547 EndZ=0
    g5: LineSegment StartX=2 StartY=1.1547 StartZ=0 EndX=0 EndY=2.3094 EndZ=0
    g6: Circle [constr] CenterX=0 CenterY=0 CenterZ=0 NormalX=0 NormalY=0 NormalZ=1 AngleXU=0 Radius=2.3094
    g7: Circle CenterX=0 CenterY=0 CenterZ=0 NormalX=0 NormalY=0 NormalZ=1 AngleXU=0 Radius=1
  constraints (18):
    c: Coincident(g0,g1)
    c: Coincident(g1,g2)
    c: Coincident(g2,g3)
    c: Coincident(g3,g4)
    c: Coincident(g4,g5)
    c: Coincident(g5,g0)
    c: Equal(g0, g1-g5) x5
    c: PointOnObject(g0,g6)
    c: PointOnObject(g1,g6)
    c: PointOnObject(g2,g6)
    c: PointOnObject(g3,g6)
    c: PointOnObject(g4,g6)
    c: PointOnObject(g5,g6)
    c: Coincident(g6,g-1)
    c: PointOnObject(g5,g-2)
    c: DistanceX(g0,g4) = 4
    c: Coincident(g7,g-1)
    c: Radius(g7) = 1
FEATURE [Sketcher::SketchObject] Sketch1155
  MapMode = 5
  Support = -> [XY_Plane560]
  sketch-geometry (1):
    g0: Circle CenterX=0 CenterY=0 CenterZ=0 NormalX=0 NormalY=0 NormalZ=1 AngleXU=0 Radius=1.9
  constraints (2):
    c: Coincident(g0,g-1)
    c: Radius(g0) = 1.9
FEATURE [Sketcher::SketchObject] Sketch1156
  MapMode = 5
  Support = -> [XY_Plane569]
  sketch-geometry (8):
    g0: LineSegment StartX=0 StartY=2.3094 StartZ=0 EndX=-2 EndY=1.1547 EndZ=0
    g1: LineSegment StartX=-2 StartY=1.1547 StartZ=0 EndX=-2 EndY=-1.1547 EndZ=0
    g2: LineSegment StartX=-2 StartY=-1.1547 StartZ=0 EndX=-2e-16 EndY=-2.3094 EndZ=0
    g3: LineSegment StartX=-2e-16 StartY=-2.3094 StartZ=0 EndX=2 EndY=-1.1547 EndZ=0
    g4: LineSegment StartX=2 StartY=-1.1547 StartZ=0 EndX=2 EndY=1.1547 EndZ=0
    g5: LineSegment StartX=2 StartY=1.1547 StartZ=0 EndX=0 EndY=2.3094 EndZ=0
    g6: Circle [constr] CenterX=0 CenterY=0 CenterZ=0 NormalX=0 NormalY=0 NormalZ=1 AngleXU=0 Radius=2.3094
    g7: Circle CenterX=0 CenterY=0 CenterZ=0 NormalX=0 NormalY=0 NormalZ=1 AngleXU=0 Radius=1
  constraints (18):
    c: Coincident(g0,g1)
    c: Coincident(g1,g2)
    c: Coincident(g2,g3)
    c: Coincident(g3,g4)
    c: Coincident(g4,g5)
    c: Coincident(g5,g0)
    c: Equal(g0, g1-g5) x5
    c: PointOnObject(g0,g6)
    c: PointOnObject(g1,g6)
    c: PointOnObject(g2,g6)
    c: PointOnObject(g3,g6)
    c: PointOnObject(g4,g6)
    c: PointOnObject(g5,g6)
    c: Coincident(g6,g-1)
    c: PointOnObject(g5,g-2)
    c: DistanceX(g0,g4) = 4
    c: Coincident(g7,g-1)
    c: Radius(g7) = 1
FEATURE [Sketcher::SketchObject] Sketch1159
  MapMode = 5
  Support = -> [XY_Plane555]
  sketch-geometry (1):
    g0: Circle CenterX=0 CenterY=0 CenterZ=0 NormalX=0 NormalY=0 NormalZ=1 AngleXU=0 Radius=1.9
  constraints (2):
    c: Coincident(g0,g-1)
    c: Radius(g0) = 1.9
FEATURE [Sketcher::SketchObject] Sketch1163
  MapMode = 5
  Placement = pos=(0,0,0) rot=(1,0,0;1.5708rad)
  Support = -> [XZ_Plane487]
  sketch-geometry (2):
    g0: Circle [constr] CenterX=0 CenterY=0 CenterZ=0 NormalX=0 NormalY=0 NormalZ=1 AngleXU=0 Radius=20
    g1: Circle CenterX=-20 CenterY=0 CenterZ=0 NormalX=0 NormalY=0 NormalZ=1 AngleXU=0 Radius=1.25
  constraints (5):
    c: Coincident(g0,g-1)
    c: Radius(g0) = 20
    c: PointOnObject(g1,g0)
    c: Radius(g1) = 1.25
    c: PointOnObject(g1,g-1)
FEATURE [Sketcher::SketchObject] Sketch1166
  MapMode = 5
  Support = -> [XY_Plane543]
FEATURE [Sketcher::SketchObject] Sketch1169
  MapMode = 5
  Support = -> [XY_Plane557]
FEATURE [Sketcher::SketchObject] Sketch1173
  MapMode = 5
  Support = -> [XY_Plane466]
  sketch-geometry (1):
    g0: Circle CenterX=0 CenterY=0 CenterZ=0 NormalX=0 NormalY=0 NormalZ=1 AngleXU=0 Radius=2.75
  constraints (2):
    c: Coincident(g0,g-1)
    c: Radius(g0) = 2.75
FEATURE [Sketcher::SketchObject] Sketch1174
  MapMode = 5
  Support = -> [XY_Plane418]
  sketch-geometry (8):
    g0: LineSegment StartX=0 StartY=3.17543 StartZ=0 EndX=-2.75 EndY=1.58771 EndZ=0
    g1: LineSegment StartX=-2.75 StartY=1.58771 StartZ=0 EndX=-2.75 EndY=-1.58771 EndZ=0
    g2: LineSegment StartX=-2.75 StartY=-1.58771 StartZ=0 EndX=0 EndY=-3.17543 EndZ=0
    g3: LineSegment StartX=0 StartY=-3.17543 StartZ=0 EndX=2.75 EndY=-1.58771 EndZ=0
    g4: LineSegment StartX=2.75 StartY=-1.58771 StartZ=0 EndX=2.75 EndY=1.58771 EndZ=0
    g5: LineSegment StartX=2.75 StartY=1.58771 StartZ=0 EndX=0 EndY=3.17543 EndZ=0
    g6: Circle [constr] CenterX=0 CenterY=0 CenterZ=0 NormalX=0 NormalY=0 NormalZ=1 AngleXU=0 Radius=3.17543
    g7: Circle CenterX=0 CenterY=0 CenterZ=0 NormalX=0 NormalY=0 NormalZ=1 AngleXU=0 Radius=1.5
  constraints (18):
    c: Coincident(g0,g1)
    c: Coincident(g1,g2)
    c: Coincident(g2,g3)
    c: Coincident(g3,g4)
    c: Coincident(g4,g5)
    c: Coincident(g5,g0)
    c: Equal(g0, g1-g5) x5
    c: PointOnObject(g0,g6)
    c: PointOnObject(g1,g6)
    c: PointOnObject(g2,g6)
    c: PointOnObject(g3,g6)
    c: PointOnObject(g4,g6)
    c: PointOnObject(g5,g6)
    c: Coincident(g6,g-1)
    c: PointOnObject(g5,g-2)
    c: DistanceX(g0,g4) = 5.5
    c: Coincident(g7,g-1)
    c: Radius(g7) = 1.5
FEATURE [Sketcher::SketchObject] Sketch1178
  MapMode = 5
  Support = -> [XY_Plane419]
FEATURE [Sketcher::SketchObject] Sketch1180
  MapMode = 5
  Support = -> [XY_Plane419]
FEATURE [Sketcher::SketchObject] Sketch1181
  MapMode = 5
  Support = -> [XY_Plane422]
  sketch-geometry (1):
    g0: Circle CenterX=0 CenterY=0 CenterZ=0 NormalX=0 NormalY=0 NormalZ=1 AngleXU=0 Radius=1.9
  constraints (2):
    c: Coincident(g0,g-1)
    c: Radius(g0) = 1.9
FEATURE [Sketcher::SketchObject] Sketch1183
  MapMode = 5
  Support = -> [XY_Plane537]
  sketch-geometry (1):
    g0: Circle CenterX=0 CenterY=0 CenterZ=0 NormalX=0 NormalY=0 NormalZ=1 AngleXU=0 Radius=2.75
  constraints (2):
    c: Coincident(g0,g-1)
    c: Radius(g0) = 2.75
FEATURE [Sketcher::SketchObject] Sketch1187
  MapMode = 5
  Placement = pos=(0,0,0) rot=(0.57735,0.57735,0.57735;2.0944rad)
  Support = -> [YZ_Plane507]
  sketch-geometry (1):
    g0: LineSegment StartX=0 StartY=0 StartZ=0 EndX=0 EndY=190 EndZ=0
  constraints (3):
    c: Coincident(g0,g-1)
    c: Vertical(g0)
    c: DistanceY(g0,g0) = 190
FEATURE [Sketcher::SketchObject] Sketch1192
  MapMode = 5
  Support = -> [XY_Plane412]
  sketch-geometry (1):
    g0: Circle CenterX=0 CenterY=0 CenterZ=0 NormalX=0 NormalY=0 NormalZ=1 AngleXU=0 Radius=2.75
  constraints (2):
    c: Coincident(g0,g-1)
    c: Radius(g0) = 2.75
FEATURE [Sketcher::SketchObject] Sketch1196
  MapMode = 5
  Support = -> [XY_Plane507]
  sketch-geometry (4):
    g0: LineSegment StartX=-10 StartY=20.15 StartZ=0 EndX=10 EndY=20.15 EndZ=0
    g1: LineSegment StartX=10 StartY=20.15 StartZ=0 EndX=10 EndY=-20.15 EndZ=0
    g2: LineSegment StartX=10 StartY=-20.15 StartZ=0 EndX=-10 EndY=-20.15 EndZ=0
    g3: LineSegment StartX=-10 StartY=-20.15 StartZ=0 EndX=-10 EndY=20.15 EndZ=0
  constraints (10):
    c: Coincident(g0,g1)
    c: Coincident(g1,g2)
    c: Coincident(g2,g3)
    c: Coincident(g3,g0)
    c: Horizontal(g2)
    c: Vertical(g3)
    c: DistanceX(g0,g0) = 20
    c: DistanceY(g1,g1) = 40.3
    c: Symmetric(g0,g1,g-1)
    c: Symmetric(g0,g0,g-2)
FEATURE [Sketcher::SketchObject] Sketch1209
  MapMode = 5
  Placement = pos=(0,0,0) rot=(1,0,0;1.5708rad)
  Support = -> [XZ_Plane521]
  sketch-geometry (1):
    g0: Circle CenterX=-1.55 CenterY=4 CenterZ=0 NormalX=0 NormalY=0 NormalZ=1 AngleXU=0 Radius=0.75
  constraints (3):
    c: Radius(g0) = 0.75
    c: DistanceY(g-1,g0) = 4
    c: DistanceX(g0,g-1) = 1.55
FEATURE [Sketcher::SketchObject] Sketch1210
  MapMode = 5
  Placement = pos=(0,0,0) rot=(1,0,0;1.5708rad)
  Support = -> [XZ_Plane422]
  sketch-geometry (1):
    g0: Circle CenterX=0 CenterY=4 CenterZ=0 NormalX=0 NormalY=0 NormalZ=1 AngleXU=0 Radius=0.75
  constraints (3):
    c: PointOnObject(g0,g-2)
    c: Radius(g0) = 0.75
    c: DistanceY(g-1,g0) = 4
FEATURE [Sketcher::SketchObject] Sketch1211
  MapMode = 5
  Support = -> [XY_Plane428]
  sketch-geometry (8):
    g0: LineSegment StartX=0 StartY=3.17543 StartZ=0 EndX=-2.75 EndY=1.58771 EndZ=0
    g1: LineSegment StartX=-2.75 StartY=1.58771 StartZ=0 EndX=-2.75 EndY=-1.58771 EndZ=0
    g2: LineSegment StartX=-2.75 StartY=-1.58771 StartZ=0 EndX=0 EndY=-3.17543 EndZ=0
    g3: LineSegment StartX=0 StartY=-3.17543 StartZ=0 EndX=2.75 EndY=-1.58771 EndZ=0
    g4: LineSegment StartX=2.75 StartY=-1.58771 StartZ=0 EndX=2.75 EndY=1.58771 EndZ=0
    g5: LineSegment StartX=2.75 StartY=1.58771 StartZ=0 EndX=0 EndY=3.17543 EndZ=0
    g6: Circle [constr] CenterX=0 CenterY=0 CenterZ=0 NormalX=0 NormalY=0 NormalZ=1 AngleXU=0 Radius=3.17543
    g7: Circle CenterX=0 CenterY=0 CenterZ=0 NormalX=0 NormalY=0 NormalZ=1 AngleXU=0 Radius=1.5
  constraints (18):
    c: Coincident(g0,g1)
    c: Coincident(g1,g2)
    c: Coincident(g2,g3)
    c: Coincident(g3,g4)
    c: Coincident(g4,g5)
    c: Coincident(g5,g0)
    c: Equal(g0, g1-g5) x5
    c: PointOnObject(g0,g6)
    c: PointOnObject(g1,g6)
    c: PointOnObject(g2,g6)
    c: PointOnObject(g3,g6)
    c: PointOnObject(g4,g6)
    c: PointOnObject(g5,g6)
    c: Coincident(g6,g-1)
    c: PointOnObject(g5,g-2)
    c: DistanceX(g0,g4) = 5.5
    c: Coincident(g7,g-1)
    c: Radius(g7) = 1.5
FEATURE [Sketcher::SketchObject] Sketch1213
  MapMode = 5
  Support = -> [XY_Plane451]
  sketch-geometry (1):
    g0: Circle CenterX=0 CenterY=0 CenterZ=0 NormalX=0 NormalY=0 NormalZ=1 AngleXU=0 Radius=2.75
  constraints (2):
    c: Coincident(g0,g-1)
    c: Radius(g0) = 2.75
FEATURE [Sketcher::SketchObject] Sketch1214
  MapMode = 5
  Support = -> [XY_Plane438]
  sketch-geometry (8):
    g0: LineSegment StartX=0 StartY=3.17543 StartZ=0 EndX=-2.75 EndY=1.58771 EndZ=0
    g1: LineSegment StartX=-2.75 StartY=1.58771 StartZ=0 EndX=-2.75 EndY=-1.58771 EndZ=0
    g2: LineSegment StartX=-2.75 StartY=-1.58771 StartZ=0 EndX=0 EndY=-3.17543 EndZ=0
    g3: LineSegment StartX=0 StartY=-3.17543 StartZ=0 EndX=2.75 EndY=-1.58771 EndZ=0
    g4: LineSegment StartX=2.75 StartY=-1.58771 StartZ=0 EndX=2.75 EndY=1.58771 EndZ=0
    g5: LineSegment StartX=2.75 StartY=1.58771 StartZ=0 EndX=0 EndY=3.17543 EndZ=0
    g6: Circle [constr] CenterX=0 CenterY=0 CenterZ=0 NormalX=0 NormalY=0 NormalZ=1 AngleXU=0 Radius=3.17543
    g7: Circle CenterX=0 CenterY=0 CenterZ=0 NormalX=0 NormalY=0 NormalZ=1 AngleXU=0 Radius=1.5
  constraints (18):
    c: Coincident(g0,g1)
    c: Coincident(g1,g2)
    c: Coincident(g2,g3)
    c: Coincident(g3,g4)
    c: Coincident(g4,g5)
    c: Coincident(g5,g0)
    c: Equal(g0, g1-g5) x5
    c: PointOnObject(g0,g6)
    c: PointOnObject(g1,g6)
    c: PointOnObject(g2,g6)
    c: PointOnObject(g3,g6)
    c: PointOnObject(g4,g6)
    c: PointOnObject(g5,g6)
    c: Coincident(g6,g-1)
    c: PointOnObject(g5,g-2)
    c: DistanceX(g0,g4) = 5.5
    c: Coincident(g7,g-1)
    c: Radius(g7) = 1.5
FEATURE [Sketcher::SketchObject] Sketch1216
  MapMode = 5
  Support = -> [XY_Plane425]
  sketch-geometry (1):
    g0: Circle CenterX=0 CenterY=0 CenterZ=0 NormalX=0 NormalY=0 NormalZ=1 AngleXU=0 Radius=2.75
  constraints (2):
    c: Coincident(g0,g-1)
    c: Radius(g0) = 2.75
FEATURE [Sketcher::SketchObject] Sketch1219
  MapMode = 5
  Support = -> [XY_Plane427]
  sketch-geometry (8):
    g0: LineSegment StartX=0 StartY=3.17543 StartZ=0 EndX=-2.75 EndY=1.58771 EndZ=0
    g1: LineSegment StartX=-2.75 StartY=1.58771 StartZ=0 EndX=-2.75 EndY=-1.58771 EndZ=0
    g2: LineSegment StartX=-2.75 StartY=-1.58771 StartZ=0 EndX=0 EndY=-3.17543 EndZ=0
    g3: LineSegment StartX=0 StartY=-3.17543 StartZ=0 EndX=2.75 EndY=-1.58771 EndZ=0
    g4: LineSegment StartX=2.75 StartY=-1.58771 StartZ=0 EndX=2.75 EndY=1.58771 EndZ=0
    g5: LineSegment StartX=2.75 StartY=1.58771 StartZ=0 EndX=0 EndY=3.17543 EndZ=0
    g6: Circle [constr] CenterX=0 CenterY=0 CenterZ=0 NormalX=0 NormalY=0 NormalZ=1 AngleXU=0 Radius=3.17543
    g7: Circle CenterX=0 CenterY=0 CenterZ=0 NormalX=0 NormalY=0 NormalZ=1 AngleXU=0 Radius=1.5
  constraints (18):
    c: Coincident(g0,g1)
    c: Coincident(g1,g2)
    c: Coincident(g2,g3)
    c: Coincident(g3,g4)
    c: Coincident(g4,g5)
    c: Coincident(g5,g0)
    c: Equal(g0, g1-g5) x5
    c: PointOnObject(g0,g6)
    c: PointOnObject(g1,g6)
    c: PointOnObject(g2,g6)
    c: PointOnObject(g3,g6)
    c: PointOnObject(g4,g6)
    c: PointOnObject(g5,g6)
    c: Coincident(g6,g-1)
    c: PointOnObject(g5,g-2)
    c: DistanceX(g0,g4) = 5.5
    c: Coincident(g7,g-1)
    c: Radius(g7) = 1.5
FEATURE [Sketcher::SketchObject] Sketch1220
  MapMode = 5
  Support = -> [XY_Plane434]
  sketch-geometry (1):
    g0: Circle CenterX=0 CenterY=0 CenterZ=0 NormalX=0 NormalY=0 NormalZ=1 AngleXU=0 Radius=2.75
  constraints (2):
    c: Coincident(g0,g-1)
    c: Radius(g0) = 2.75
FEATURE [Sketcher::SketchObject] Sketch1221
  MapMode = 5
  Support = -> [XY_Plane520]
  sketch-geometry (1):
    g0: Circle CenterX=0 CenterY=10.15 CenterZ=0 NormalX=0 NormalY=0 NormalZ=1 AngleXU=0 Radius=3
  constraints (3):
    c: PointOnObject(g0,g-2)
    c: DistanceY(g-1,g0) = 10.15
    c: Radius(g0) = 3
FEATURE [Sketcher::SketchObject] Sketch1223
  MapMode = 5
  Support = -> [XY_Plane417]
  sketch-geometry (8):
    g0: LineSegment StartX=0 StartY=3.17543 StartZ=0 EndX=-2.75 EndY=1.58771 EndZ=0
    g1: LineSegment StartX=-2.75 StartY=1.58771 StartZ=0 EndX=-2.75 EndY=-1.58771 EndZ=0
    g2: LineSegment StartX=-2.75 StartY=-1.58771 StartZ=0 EndX=0 EndY=-3.17543 EndZ=0
    g3: LineSegment StartX=0 StartY=-3.17543 StartZ=0 EndX=2.75 EndY=-1.58771 EndZ=0
    g4: LineSegment StartX=2.75 StartY=-1.58771 StartZ=0 EndX=2.75 EndY=1.58771 EndZ=0
    g5: LineSegment StartX=2.75 StartY=1.58771 StartZ=0 EndX=0 EndY=3.17543 EndZ=0
    g6: Circle [constr] CenterX=0 CenterY=0 CenterZ=0 NormalX=0 NormalY=0 NormalZ=1 AngleXU=0 Radius=3.17543
    g7: Circle CenterX=0 CenterY=0 CenterZ=0 NormalX=0 NormalY=0 NormalZ=1 AngleXU=0 Radius=1.5
  constraints (18):
    c: Coincident(g0,g1)
    c: Coincident(g1,g2)
    c: Coincident(g2,g3)
    c: Coincident(g3,g4)
    c: Coincident(g4,g5)
    c: Coincident(g5,g0)
    c: Equal(g0, g1-g5) x5
    c: PointOnObject(g0,g6)
    c: PointOnObject(g1,g6)
    c: PointOnObject(g2,g6)
    c: PointOnObject(g3,g6)
    c: PointOnObject(g4,g6)
    c: PointOnObject(g5,g6)
    c: Coincident(g6,g-1)
    c: PointOnObject(g5,g-2)
    c: DistanceX(g0,g4) = 5.5
    c: Coincident(g7,g-1)
    c: Radius(g7) = 1.5
FEATURE [Sketcher::SketchObject] Sketch1226
  MapMode = 5
  Placement = pos=(0,0,0) rot=(1,0,0;1.5708rad)
  Support = -> [XZ_Plane515]
  sketch-geometry (1):
    g0: Circle CenterX=1.55 CenterY=4 CenterZ=0 NormalX=0 NormalY=0 NormalZ=1 AngleXU=0 Radius=0.75
  constraints (3):
    c: Radius(g0) = 0.75
    c: DistanceY(g-1,g0) = 4
    c: DistanceX(g-1,g0) = 1.55
FEATURE [Sketcher::SketchObject] Sketch1231
  MapMode = 5
  Placement = pos=(0,0,0) rot=(1,0,0;1.5708rad)
  Support = -> [XZ_Plane446]
  sketch-geometry (8):
    g0: LineSegment StartX=-1.5 StartY=2.25 StartZ=0 EndX=-3.25 EndY=2.25 EndZ=0
    g1: LineSegment StartX=-3.25 StartY=2.25 StartZ=0 EndX=-3.25 EndY=1.25 EndZ=0
    g2: LineSegment StartX=-3.25 StartY=1.25 StartZ=0 EndX=-2 EndY=1.25 EndZ=0
    g3: LineSegment StartX=-2 StartY=1.25 StartZ=0 EndX=-2 EndY=-1.25 EndZ=0
    g4: LineSegment StartX=-2 StartY=-1.25 StartZ=0 EndX=-3.25 EndY=-1.25 EndZ=0
    g5: LineSegment StartX=-3.25 StartY=-1.25 StartZ=0 EndX=-3.25 EndY=-2.25 EndZ=0
    g6: LineSegment StartX=-3.25 StartY=-2.25 StartZ=0 EndX=-1.5 EndY=-2.25 EndZ=0
    g7: LineSegment StartX=-1.5 StartY=-2.25 StartZ=0 EndX=-1.5 EndY=2.25 EndZ=0
  constraints (23):
    c: Horizontal(g0)
    c: Coincident(g0,g1)
    c: Vertical(g1)
    c: Coincident(g1,g2)
    c: Horizontal(g2)
    c: Coincident(g2,g3)
    c: Vertical(g3)
    c: Coincident(g3,g4)
    c: Horizontal(g4)
    c: Coincident(g4,g5)
    c: Vertical(g5)
    c: Coincident(g5,g6)
    c: Horizontal(g6)
    c: Coincident(g6,g7)
    c: Vertical(g7)
    c: Coincident(g0,g7)
    c: Equal(g1,g5)
    c: Symmetric(g4,g1,g-1)
    c: DistanceX(g0,g-1) = 1.5
    c: DistanceY(g3,g3) = 2.5
    c: DistanceY(g7,g7) = 4.5
    c: DistanceX(g0,g-1) = 3.25
    c: DistanceX(g2,g-1) = 2
FEATURE [Sketcher::SketchObject] Sketch1232
  MapMode = 5
  Support = -> [XY_Plane421]
FEATURE [Sketcher::SketchObject] Sketch1233
  MapMode = 5
  Placement = pos=(0,0,0) rot=(1,0,0;1.5708rad)
  Support = -> [XZ_Plane450]
  sketch-geometry (8):
    g0: LineSegment StartX=-1.5 StartY=2.25 StartZ=0 EndX=-3.25 EndY=2.25 EndZ=0
    g1: LineSegment StartX=-3.25 StartY=2.25 StartZ=0 EndX=-3.25 EndY=1.25 EndZ=0
    g2: LineSegment StartX=-3.25 StartY=1.25 StartZ=0 EndX=-2 EndY=1.25 EndZ=0
    g3: LineSegment StartX=-2 StartY=1.25 StartZ=0 EndX=-2 EndY=-1.25 EndZ=0
    g4: LineSegment StartX=-2 StartY=-1.25 StartZ=0 EndX=-3.25 EndY=-1.25 EndZ=0
    g5: LineSegment StartX=-3.25 StartY=-1.25 StartZ=0 EndX=-3.25 EndY=-2.25 EndZ=0
    g6: LineSegment StartX=-3.25 StartY=-2.25 StartZ=0 EndX=-1.5 EndY=-2.25 EndZ=0
    g7: LineSegment StartX=-1.5 StartY=-2.25 StartZ=0 EndX=-1.5 EndY=2.25 EndZ=0
  constraints (23):
    c: Horizontal(g0)
    c: Coincident(g0,g1)
    c: Vertical(g1)
    c: Coincident(g1,g2)
    c: Horizontal(g2)
    c: Coincident(g2,g3)
    c: Vertical(g3)
    c: Coincident(g3,g4)
    c: Horizontal(g4)
    c: Coincident(g4,g5)
    c: Vertical(g5)
    c: Coincident(g5,g6)
    c: Horizontal(g6)
    c: Coincident(g6,g7)
    c: Vertical(g7)
    c: Coincident(g0,g7)
    c: Equal(g1,g5)
    c: Symmetric(g4,g1,g-1)
    c: DistanceX(g0,g-1) = 1.5
    c: DistanceY(g3,g3) = 2.5
    c: DistanceY(g7,g7) = 4.5
    c: DistanceX(g0,g-1) = 3.25
    c: DistanceX(g2,g-1) = 2
FEATURE [Sketcher::SketchObject] Sketch1235
  MapMode = 5
  Support = -> [XY_Plane426]
  sketch-geometry (1):
    g0: Circle CenterX=0 CenterY=0 CenterZ=0 NormalX=0 NormalY=0 NormalZ=1 AngleXU=0 Radius=2.75
  constraints (2):
    c: Coincident(g0,g-1)
    c: Radius(g0) = 2.75
FEATURE [Sketcher::SketchObject] Sketch1236
  MapMode = 5
  Placement = pos=(0,0,0) rot=(1,0,0;1.5708rad)
  Support = -> [XZ_Plane469]
  sketch-geometry (8):
    g0: LineSegment StartX=-1.5 StartY=2.25 StartZ=0 EndX=-3.25 EndY=2.25 EndZ=0
    g1: LineSegment StartX=-3.25 StartY=2.25 StartZ=0 EndX=-3.25 EndY=1.25 EndZ=0
    g2: LineSegment StartX=-3.25 StartY=1.25 StartZ=0 EndX=-2 EndY=1.25 EndZ=0
    g3: LineSegment StartX=-2 StartY=1.25 StartZ=0 EndX=-2 EndY=-1.25 EndZ=0
    g4: LineSegment StartX=-2 StartY=-1.25 StartZ=0 EndX=-3.25 EndY=-1.25 EndZ=0
    g5: LineSegment StartX=-3.25 StartY=-1.25 StartZ=0 EndX=-3.25 EndY=-2.25 EndZ=0
    g6: LineSegment StartX=-3.25 StartY=-2.25 StartZ=0 EndX=-1.5 EndY=-2.25 EndZ=0
    g7: LineSegment StartX=-1.5 StartY=-2.25 StartZ=0 EndX=-1.5 EndY=2.25 EndZ=0
  constraints (23):
    c: Horizontal(g0)
    c: Coincident(g0,g1)
    c: Vertical(g1)
    c: Coincident(g1,g2)
    c: Horizontal(g2)
    c: Coincident(g2,g3)
    c: Vertical(g3)
    c: Coincident(g3,g4)
    c: Horizontal(g4)
    c: Coincident(g4,g5)
    c: Vertical(g5)
    c: Coincident(g5,g6)
    c: Horizontal(g6)
    c: Coincident(g6,g7)
    c: Vertical(g7)
    c: Coincident(g0,g7)
    c: Equal(g1,g5)
    c: Symmetric(g4,g1,g-1)
    c: DistanceX(g0,g-1) = 1.5
    c: DistanceY(g3,g3) = 2.5
    c: DistanceY(g7,g7) = 4.5
    c: DistanceX(g0,g-1) = 3.25
    c: DistanceX(g2,g-1) = 2
FEATURE [Sketcher::SketchObject] Sketch1237
  MapMode = 5
  Placement = pos=(0,0,0) rot=(1,0,0;1.5708rad)
  Support = -> [XZ_Plane462]
  sketch-geometry (8):
    g0: LineSegment StartX=-1.5 StartY=2.25 StartZ=0 EndX=-3.25 EndY=2.25 EndZ=0
    g1: LineSegment StartX=-3.25 StartY=2.25 StartZ=0 EndX=-3.25 EndY=1.25 EndZ=0
    g2: LineSegment StartX=-3.25 StartY=1.25 StartZ=0 EndX=-2 EndY=1.25 EndZ=0
    g3: LineSegment StartX=-2 StartY=1.25 StartZ=0 EndX=-2 EndY=-1.25 EndZ=0
    g4: LineSegment StartX=-2 StartY=-1.25 StartZ=0 EndX=-3.25 EndY=-1.25 EndZ=0
    g5: LineSegment StartX=-3.25 StartY=-1.25 StartZ=0 EndX=-3.25 EndY=-2.25 EndZ=0
    g6: LineSegment StartX=-3.25 StartY=-2.25 StartZ=0 EndX=-1.5 EndY=-2.25 EndZ=0
    g7: LineSegment StartX=-1.5 StartY=-2.25 StartZ=0 EndX=-1.5 EndY=2.25 EndZ=0
  constraints (23):
    c: Horizontal(g0)
    c: Coincident(g0,g1)
    c: Vertical(g1)
    c: Coincident(g1,g2)
    c: Horizontal(g2)
    c: Coincident(g2,g3)
    c: Vertical(g3)
    c: Coincident(g3,g4)
    c: Horizontal(g4)
    c: Coincident(g4,g5)
    c: Vertical(g5)
    c: Coincident(g5,g6)
    c: Horizontal(g6)
    c: Coincident(g6,g7)
    c: Vertical(g7)
    c: Coincident(g0,g7)
    c: Equal(g1,g5)
    c: Symmetric(g4,g1,g-1)
    c: DistanceX(g0,g-1) = 1.5
    c: DistanceY(g3,g3) = 2.5
    c: DistanceY(g7,g7) = 4.5
    c: DistanceX(g0,g-1) = 3.25
    c: DistanceX(g2,g-1) = 2
FEATURE [Sketcher::SketchObject] Sketch1238
  MapMode = 5
  Support = -> [XY_Plane540]
FEATURE [Sketcher::SketchObject] Sketch1239
  MapMode = 5
  Support = -> [XY_Plane442]
  sketch-geometry (8):
    g0: LineSegment StartX=-16.75 StartY=28.25 StartZ=0 EndX=16.75 EndY=28.25 EndZ=0
    g1: LineSegment StartX=21.75 StartY=23.25 StartZ=0 EndX=21.75 EndY=-23.25 EndZ=0
    g2: LineSegment StartX=16.75 StartY=-28.25 StartZ=0 EndX=-16.75 EndY=-28.25 EndZ=0
    g3: LineSegment StartX=-21.75 StartY=-23.25 StartZ=0 EndX=-21.75 EndY=23.25 EndZ=0
    g4: ArcOfCircle CenterX=-16.75 CenterY=23.25 CenterZ=0 NormalX=0 NormalY=0 NormalZ=1 AngleXU=0 Radius=5 StartAngle=1.5708 EndAngle=3.14159
    g5: ArcOfCircle CenterX=16.75 CenterY=23.25 CenterZ=0 NormalX=0 NormalY=0 NormalZ=1 AngleXU=0 Radius=5 StartAngle=1e-16 EndAngle=1.5708
    g6: ArcOfCircle CenterX=16.75 CenterY=-23.25 CenterZ=0 NormalX=0 NormalY=0 NormalZ=1 AngleXU=0 Radius=5 StartAngle=4.71239 EndAngle=6.28319
    g7: ArcOfCircle CenterX=-16.75 CenterY=-23.25 CenterZ=0 NormalX=0 NormalY=0 NormalZ=1 AngleXU=0 Radius=5 StartAngle=3.14159 EndAngle=4.71239
  constraints (18):
    c: Horizontal(g2)
    c: Vertical(g1)
    c: Tangent(g3,g4) = 1.5708
    c: Tangent(g0,g4) = 1.5708
    c: Tangent(g0,g5) = 1.5708
    c: Tangent(g1,g5) = 1.5708
    c: Tangent(g1,g6) = 1.5708
    c: Tangent(g2,g6) = 1.5708
    c: Tangent(g2,g7) = 1.5708
    c: Tangent(g3,g7) = 1.5708
    c: Equal(g4,g5)
    c: Equal(g5,g7)
    c: Equal(g7,g6)
    c: Radius(g5) = 5
    c: DistanceY(g2,g0) = 56.5
    c: DistanceX(g3,g1) = 43.5
    c: Symmetric(g0,g0,g-2)
    c: Symmetric(g3,g3,g-1)
FEATURE [Sketcher::SketchObject] Sketch1240
  MapMode = 5
  Support = -> [XY_Plane452]
FEATURE [Sketcher::SketchObject] Sketch1241
  MapMode = 5
  Support = -> [XY_Plane452]
FEATURE [Sketcher::SketchObject] Sketch1242
  MapMode = 5
  Support = -> [XY_Plane420]
  sketch-geometry (13):
    g0: Circle [constr] CenterX=0 CenterY=0 CenterZ=0 NormalX=0 NormalY=0 NormalZ=1 AngleXU=0 Radius=20
    g1: LineSegment [constr] StartX=-14.1421 StartY=14.1421 StartZ=0 EndX=14.1421 EndY=14.1421 EndZ=0
    g2: LineSegment [constr] StartX=14.1421 StartY=14.1421 StartZ=0 EndX=14.1421 EndY=-14.1421 EndZ=0
    g3: LineSegment [constr] StartX=14.1421 StartY=-14.1421 StartZ=0 EndX=-14.1421 EndY=-14.1421 EndZ=0
    g4: LineSegment [constr] StartX=-14.1421 StartY=-14.1421 StartZ=0 EndX=-14.1421 EndY=14.1421 EndZ=0
    g5: ArcOfCircle CenterX=0 CenterY=0 CenterZ=0 NormalX=0 NormalY=0 NormalZ=1 AngleXU=0 Radius=20 StartAngle=2.60685 EndAngle=3.67634
    g6: ArcOfCircle CenterX=-14.1421 CenterY=14.1421 CenterZ=0 NormalX=0 NormalY=0 NormalZ=1 AngleXU=0 Radius=5 StartAngle=0.66007 EndAngle=4.05232
    g7: ArcOfCircle CenterX=14.1421 CenterY=14.1421 CenterZ=0 NormalX=0 NormalY=0 NormalZ=1 AngleXU=0 Radius=5 StartAngle=5.37246 EndAngle=8.76471
    g8: ArcOfCircle CenterX=14.1421 CenterY=-14.1421 CenterZ=0 NormalX=0 NormalY=0 NormalZ=1 AngleXU=0 Radius=5 StartAngle=3.80166 EndAngle=7.19391
    g9: ArcOfCircle CenterX=-14.1421 CenterY=-14.1421 CenterZ=0 NormalX=0 NormalY=0 NormalZ=1 AngleXU=0 Radius=5 StartAngle=2.23087 EndAngle=5.62311
    g10: ArcOfCircle CenterX=0 CenterY=0 CenterZ=0 NormalX=0 NormalY=0 NormalZ=1 AngleXU=0 Radius=20 StartAngle=1.03605 EndAngle=2.10554
    g11: ArcOfCircle CenterX=0 CenterY=0 CenterZ=0 NormalX=0 NormalY=0 NormalZ=1 AngleXU=0 Radius=20 StartAngle=5.74844 EndAngle=6.81793
    g12: ArcOfCircle CenterX=0 CenterY=0 CenterZ=0 NormalX=0 NormalY=0 NormalZ=1 AngleXU=0 Radius=20 StartAngle=4.17765 EndAngle=5.24713
  constraints (38):
    c: Coincident(g0,g-1)
    c: Radius(g0) = 20
    c: Coincident(g1,g2)
    c: Coincident(g2,g3)
    c: Coincident(g3,g4)
    c: Coincident(g4,g1)
    c: Horizontal(g1)
    c: Horizontal(g3)
    c: Vertical(g2)
    c: Vertical(g4)
    c: PointOnObject(g1,g0)
    c: PointOnObject(g2,g0)
    c: Equal(g1,g2)
    c: PointOnObject(g1,g0)
    c: Coincident(g5,g-1)
    c: Radius(g5) = 20
    c: Coincident(g6,g1)
    c: Coincident(g7,g1)
    c: Coincident(g8,g2)
    c: Coincident(g9,g3)
    c: Coincident(g5,g6)
    c: Equal(g5,g10)
    c: Coincident(g10,g7)
    c: Coincident(g5,g10)
    c: Coincident(g11,g7)
    c: Equal(g5,g11)
    c: Coincident(g11,g8)
    c: Coincident(g5,g11)
    c: Coincident(g12,g8)
    c: Equal(g5,g12)
    c: Coincident(g12,g9)
    c: Coincident(g5,g12)
    c: Coincident(g5,g9)
    c: Coincident(g6,g10)
    c: Radius(g6) = 5
    c: Equal(g6,g7)
    c: Equal(g6,g8)
    c: Equal(g6,g9)
FEATURE [Sketcher::SketchObject] Sketch1244
  MapMode = 5
  Support = -> [XY_Plane508]
  sketch-geometry (8):
    g0: LineSegment StartX=0 StartY=2.3094 StartZ=0 EndX=-2 EndY=1.1547 EndZ=0
    g1: LineSegment StartX=-2 StartY=1.1547 StartZ=0 EndX=-2 EndY=-1.1547 EndZ=0
    g2: LineSegment StartX=-2 StartY=-1.1547 StartZ=0 EndX=-2e-16 EndY=-2.3094 EndZ=0
    g3: LineSegment StartX=-2e-16 StartY=-2.3094 StartZ=0 EndX=2 EndY=-1.1547 EndZ=0
    g4: LineSegment StartX=2 StartY=-1.1547 StartZ=0 EndX=2 EndY=1.1547 EndZ=0
    g5: LineSegment StartX=2 StartY=1.1547 StartZ=0 EndX=0 EndY=2.3094 EndZ=0
    g6: Circle [constr] CenterX=0 CenterY=0 CenterZ=0 NormalX=0 NormalY=0 NormalZ=1 AngleXU=0 Radius=2.3094
    g7: Circle CenterX=0 CenterY=0 CenterZ=0 NormalX=0 NormalY=0 NormalZ=1 AngleXU=0 Radius=1
  constraints (18):
    c: Coincident(g0,g1)
    c: Coincident(g1,g2)
    c: Coincident(g2,g3)
    c: Coincident(g3,g4)
    c: Coincident(g4,g5)
    c: Coincident(g5,g0)
    c: Equal(g0, g1-g5) x5
    c: PointOnObject(g0,g6)
    c: PointOnObject(g1,g6)
    c: PointOnObject(g2,g6)
    c: PointOnObject(g3,g6)
    c: PointOnObject(g4,g6)
    c: PointOnObject(g5,g6)
    c: Coincident(g6,g-1)
    c: PointOnObject(g5,g-2)
    c: DistanceX(g0,g4) = 4
    c: Coincident(g7,g-1)
    c: Radius(g7) = 1
FEATURE [Sketcher::SketchObject] Sketch1253
  MapMode = 5
  Support = -> [XY_Plane512]
  sketch-geometry (1):
    g0: Circle CenterX=0 CenterY=0 CenterZ=0 NormalX=0 NormalY=0 NormalZ=1 AngleXU=0 Radius=1.9
  constraints (2):
    c: Coincident(g0,g-1)
    c: Radius(g0) = 1.9
FEATURE [Sketcher::SketchObject] Sketch1256
  MapMode = 5
  Support = -> [XY_Plane530]
  sketch-geometry (64):
    g0: LineSegment [constr] StartX=-3.75 StartY=6.49519 StartZ=0 EndX=-7.5 EndY=0 EndZ=0
    g1: LineSegment [constr] StartX=-7.5 StartY=0 StartZ=0 EndX=-3.75 EndY=-6.49519 EndZ=0
    g2: LineSegment [constr] StartX=-3.75 StartY=-6.49519 StartZ=0 EndX=3.75 EndY=-6.49519 EndZ=0
    g3: LineSegment [constr] StartX=3.75 StartY=-6.49519 StartZ=0 EndX=7.5 EndY=0 EndZ=0
    g4: LineSegment [constr] StartX=7.5 StartY=0 StartZ=0 EndX=3.75 EndY=6.49519 EndZ=0
    g5: LineSegment [constr] StartX=3.75 StartY=6.49519 StartZ=0 EndX=-3.75 EndY=6.49519 EndZ=0
    g6: Circle [constr] CenterX=0 CenterY=0 CenterZ=0 NormalX=0 NormalY=0 NormalZ=1 AngleXU=0 Radius=7.5
    g7: LineSegment [constr] StartX=0 StartY=7.5 StartZ=0 EndX=-6.49519 EndY=3.75 EndZ=0
    g8: LineSegment [constr] StartX=-6.49519 StartY=3.75 StartZ=0 EndX=-6.49519 EndY=-3.75 EndZ=0
    g9: LineSegment [constr] StartX=-6.49519 StartY=-3.75 StartZ=0 EndX=9.8e-15 EndY=-7.5 EndZ=0
    g10: LineSegment [constr] StartX=9.8e-15 StartY=-7.5 StartZ=0 EndX=6.49519 EndY=-3.75 EndZ=0
    g11: LineSegment [constr] StartX=6.49519 StartY=-3.75 StartZ=0 EndX=6.49519 EndY=3.75 EndZ=0
    g12: LineSegment [constr] StartX=6.49519 StartY=3.75 StartZ=0 EndX=0 EndY=7.5 EndZ=0
    g13: Circle [constr] CenterX=0 CenterY=0 CenterZ=0 NormalX=0 NormalY=0 NormalZ=1 AngleXU=0 Radius=7.5
    g14: LineSegment [constr] StartX=0 StartY=10.5 StartZ=0 EndX=-9.09327 EndY=5.25 EndZ=0
    g15: LineSegment [constr] StartX=-9.09327 StartY=5.25 StartZ=0 EndX=-9.09327 EndY=-5.25 EndZ=0
    g16: LineSegment [constr] StartX=-9.09327 StartY=-5.25 StartZ=0 EndX=-1.42e-14 EndY=-10.5 EndZ=0
    g17: LineSegment [constr] StartX=-1.42e-14 StartY=-10.5 StartZ=0 EndX=9.09327 EndY=-5.25 EndZ=0
    g18: LineSegment [constr] StartX=9.09327 StartY=-5.25 StartZ=0 EndX=9.09327 EndY=5.25 EndZ=0
    g19: LineSegment [constr] StartX=9.09327 StartY=5.25 StartZ=0 EndX=0 EndY=10.5 EndZ=0
    g20: Circle [constr] CenterX=0 CenterY=0 CenterZ=0 NormalX=0 NormalY=0 NormalZ=1 AngleXU=0 Radius=10.5
    g21: LineSegment [constr] StartX=0 StartY=13.5 StartZ=0 EndX=-11.6913 EndY=6.75 EndZ=0
    g22: LineSegment [constr] StartX=-11.6913 StartY=6.75 StartZ=0 EndX=-11.6913 EndY=-6.75 EndZ=0
    g23: LineSegment [constr] StartX=-11.6913 StartY=-6.75 StartZ=0 EndX=0 EndY=-13.5 EndZ=0
    g24: LineSegment [constr] StartX=0 StartY=-13.5 StartZ=0 EndX=11.6913 EndY=-6.75 EndZ=0
    g25: LineSegment [constr] StartX=11.6913 StartY=-6.75 StartZ=0 EndX=11.6913 EndY=6.75 EndZ=0
    g26: LineSegment [constr] StartX=11.6913 StartY=6.75 StartZ=0 EndX=0 EndY=13.5 EndZ=0
    g27: Circle [constr] CenterX=0 CenterY=0 CenterZ=0 NormalX=0 NormalY=0 NormalZ=1 AngleXU=0 Radius=13.5
    g28: ArcOfCircle CenterX=0 CenterY=13.5 CenterZ=0 NormalX=0 NormalY=0 NormalZ=1 AngleXU=0 Radius=2.5 StartAngle=0.171439 EndAngle=2.97015
    g29: ArcOfCircle CenterX=11.6913 CenterY=6.75 CenterZ=0 NormalX=0 NormalY=0 NormalZ=1 AngleXU=0 Radius=2.5 StartAngle=5.40743 EndAngle=8.20614
    g30: ArcOfCircle CenterX=11.6913 CenterY=-6.75 CenterZ=0 NormalX=0 NormalY=0 NormalZ=1 AngleXU=0 Radius=2.5 StartAngle=4.36023 EndAngle=7.15894
    g31: ArcOfCircle CenterX=0 CenterY=-13.5 CenterZ=0 NormalX=0 NormalY=0 NormalZ=1 AngleXU=0 Radius=2.5 StartAngle=3.31303 EndAngle=6.11175
    g32: ArcOfCircle CenterX=-11.6913 CenterY=-6.75 CenterZ=0 NormalX=0 NormalY=0 NormalZ=1 AngleXU=0 Radius=2.5 StartAngle=2.26583 EndAngle=5.06455
    g33: ArcOfCircle CenterX=-11.6913 CenterY=6.75 CenterZ=0 NormalX=0 NormalY=0 NormalZ=1 AngleXU=0 Radius=2.5 StartAngle=1.21864 EndAngle=4.01735
    g34: LineSegment StartX=-10.829 StartY=9.09658 StartZ=0 EndX=-3.75 EndY=6.49519 EndZ=0
    g35: LineSegment StartX=-3.75 StartY=6.49519 StartZ=0 EndX=-2.46335 EndY=13.9265 EndZ=0
    g36: LineSegment StartX=2.46335 StartY=13.9265 StartZ=0 EndX=3.75 EndY=6.49519 EndZ=0
    g37: LineSegment StartX=3.75 StartY=6.49519 StartZ=0 EndX=10.829 EndY=9.09658 EndZ=0
    g38: LineSegment StartX=13.2924 StartY=4.82993 StartZ=0 EndX=7.5 EndY=0 EndZ=0
    g39: LineSegment StartX=7.5 StartY=0 StartZ=0 EndX=13.2924 EndY=-4.82993 EndZ=0
    g40: LineSegment StartX=10.829 StartY=-9.09658 StartZ=0 EndX=3.75 EndY=-6.49519 EndZ=0
    g41: LineSegment StartX=3.75 StartY=-6.49519 StartZ=0 EndX=2.46335 EndY=-13.9265 EndZ=0
    g42: LineSegment StartX=-2.46335 StartY=-13.9265 StartZ=0 EndX=-3.75 EndY=-6.49519 EndZ=0
    g43: LineSegment StartX=-3.75 StartY=-6.49519 StartZ=0 EndX=-10.829 EndY=-9.09658 EndZ=0
    g44: LineSegment StartX=-13.2924 StartY=-4.82993 StartZ=0 EndX=-7.5 EndY=0 EndZ=0
    g45: LineSegment StartX=-7.5 StartY=0 StartZ=0 EndX=-13.2924 EndY=4.82993 EndZ=0
    g46: Circle CenterX=-11.6913 CenterY=6.75 CenterZ=0 NormalX=0 NormalY=0 NormalZ=1 AngleXU=0 Radius=0.75
    g47: Circle CenterX=-9.09327 CenterY=5.25 CenterZ=0 NormalX=0 NormalY=0 NormalZ=1 AngleXU=0 Radius=0.75
    g48: Circle CenterX=-6.49519 CenterY=3.75 CenterZ=0 NormalX=0 NormalY=0 NormalZ=1 AngleXU=0 Radius=0.75
    g49: Circle CenterX=0 CenterY=13.5 CenterZ=0 NormalX=0 NormalY=0 NormalZ=1 AngleXU=0 Radius=0.75
    g50: Circle CenterX=0 CenterY=10.5 CenterZ=0 NormalX=0 NormalY=0 NormalZ=1 AngleXU=0 Radius=0.75
    g51: Circle CenterX=0 CenterY=7.5 CenterZ=0 NormalX=0 NormalY=0 NormalZ=1 AngleXU=0 Radius=0.75
    g52: Circle CenterX=11.6913 CenterY=6.75 CenterZ=0 NormalX=0 NormalY=0 NormalZ=1 AngleXU=0 Radius=0.75
    g53: Circle CenterX=9.09327 CenterY=5.25 CenterZ=0 NormalX=0 NormalY=0 NormalZ=1 AngleXU=0 Radius=0.75
    g54: Circle CenterX=6.49519 CenterY=3.75 CenterZ=0 NormalX=0 NormalY=0 NormalZ=1 AngleXU=0 Radius=0.75
    g55: Circle CenterX=11.6913 CenterY=-6.75 CenterZ=0 NormalX=0 NormalY=0 NormalZ=1 AngleXU=0 Radius=0.75
    g56: Circle CenterX=9.09327 CenterY=-5.25 CenterZ=0 NormalX=0 NormalY=0 NormalZ=1 AngleXU=0 Radius=0.75
    g57: Circle CenterX=6.49519 CenterY=-3.75 CenterZ=0 NormalX=0 NormalY=0 NormalZ=1 AngleXU=0 Radius=0.75
    g58: Circle CenterX=9.8e-15 CenterY=-7.5 CenterZ=0 NormalX=0 NormalY=0 NormalZ=1 AngleXU=0 Radius=0.75
    g59: Circle CenterX=-1.42e-14 CenterY=-10.5 CenterZ=0 NormalX=0 NormalY=0 NormalZ=1 AngleXU=0 Radius=0.75
    g60: Circle CenterX=0 CenterY=-13.5 CenterZ=0 NormalX=0 NormalY=0 NormalZ=1 AngleXU=0 Radius=0.75
    g61: Circle CenterX=-11.6913 CenterY=-6.75 CenterZ=0 NormalX=0 NormalY=0 NormalZ=1 AngleXU=0 Radius=0.75
    g62: Circle CenterX=-9.09327 CenterY=-5.25 CenterZ=0 NormalX=0 NormalY=0 NormalZ=1 AngleXU=0 Radius=0.75
    g63: Circle CenterX=-6.49519 CenterY=-3.75 CenterZ=0 NormalX=0 NormalY=0 NormalZ=1 AngleXU=0 Radius=0.75
  constraints (136):
    c: Coincident(g0,g1)
    c: Coincident(g1,g2)
    c: Coincident(g2,g3)
    c: Coincident(g3,g4)
    c: Coincident(g4,g5)
    c: Coincident(g5,g0)
    c: Equal(g0, g1-g5) x5
    c: PointOnObject(g0,g6)
    c: PointOnObject(g1,g6)
    c: PointOnObject(g2,g6)
    c: PointOnObject(g3,g6)
    c: PointOnObject(g4,g6)
    c: PointOnObject(g5,g6)
    c: Coincident(g6,g-1)
    c: Coincident(g7,g8)
    c: Coincident(g8,g9)
    c: Coincident(g9,g10)
    c: Coincident(g10,g11)
    c: Coincident(g11,g12)
    c: Coincident(g12,g7)
    c: Equal(g7, g8-g12) x5
    c: PointOnObject(g7,g13)
    c: PointOnObject(g8,g13)
    c: PointOnObject(g9,g13)
    c: PointOnObject(g10,g13)
    c: PointOnObject(g11,g13)
    c: PointOnObject(g12,g13)
    c: Coincident(g13,g-1)
    c: PointOnObject(g12,g6)
    c: PointOnObject(g7,g-2)
    c: Horizontal(g5)
    c: Radius(g6) = 7.5
    c: Coincident(g14,g15)
    c: Coincident(g15,g16)
    c: Coincident(g16,g17)
    c: Coincident(g17,g18)
    c: Coincident(g18,g19)
    c: Coincident(g19,g14)
    c: Equal(g14, g15-g19) x5
    c: PointOnObject(g14,g20)
    c: PointOnObject(g15,g20)
    c: PointOnObject(g16,g20)
    c: PointOnObject(g17,g20)
    c: PointOnObject(g18,g20)
    c: PointOnObject(g19,g20)
    c: Coincident(g20,g-1)
    c: PointOnObject(g19,g-2)
    c: Radius(g20) = 10.5
    c: Coincident(g21,g22)
    c: Coincident(g22,g23)
    c: Coincident(g23,g24)
    c: Coincident(g24,g25)
    c: Coincident(g25,g26)
    c: Coincident(g26,g21)
    c: Equal(g21, g22-g26) x5
    c: PointOnObject(g21,g27)
    c: PointOnObject(g22,g27)
    c: PointOnObject(g23,g27)
    c: PointOnObject(g24,g27)
    c: PointOnObject(g25,g27)
    c: PointOnObject(g26,g27)
    c: Coincident(g27,g-1)
    c: PointOnObject(g26,g-2)
    c: Radius(g27) = 13.5
    c: Coincident(g28,g21)
    c: Coincident(g29,g25)
    c: Coincident(g30,g24)
    c: Coincident(g31,g23)
    c: Coincident(g32,g22)
    c: Coincident(g33,g21)
    c: Coincident(g34,g0)
    c: Coincident(g35,g34)
    c: Coincident(g36,g4)
    c: Coincident(g37,g36)
    c: Coincident(g38,g3)
    c: Coincident(g39,g38)
    c: Coincident(g40,g2)
    c: Coincident(g41,g40)
    c: Coincident(g42,g1)
    c: Coincident(g43,g42)
    c: Coincident(g44,g0)
    c: Coincident(g45,g44)
    c: Tangent(g35,g28) = 1.5708
    c: Tangent(g36,g28) = 1.5708
    c: Tangent(g37,g29) = 1.5708
    c: Tangent(g38,g29) = 1.5708
    c: Tangent(g39,g30) = 1.5708
    c: Tangent(g40,g30) = 1.5708
    c: Tangent(g41,g31) = 1.5708
    c: Tangent(g42,g31) = 1.5708
    c: Tangent(g43,g32) = 1.5708
    c: Tangent(g44,g32) = 1.5708
    c: Tangent(g45,g33) = 1.5708
    c: Tangent(g34,g33) = 1.5708
    c: Radius(g29) = 2.5
    c: Equal(g29,g28)
    c: Equal(g28,g33)
    c: Equal(g33,g32)
    c: Equal(g32,g31)
    c: Equal(g31,g30)
    c: Coincident(g46,g33)
    c: Coincident(g47,g14)
    c: Coincident(g48,g7)
    c: Coincident(g49,g28)
    c: Coincident(g50,g14)
    c: Coincident(g51,g7)
    c: Coincident(g52,g29)
    c: Coincident(g53,g18)
    c: Coincident(g54,g11)
    c: Coincident(g55,g30)
    c: Coincident(g56,g17)
    c: Coincident(g57,g10)
    c: Coincident(g58,g9)
    c: Coincident(g59,g16)
    c: Coincident(g60,g31)
    c: Coincident(g61,g32)
    c: Coincident(g62,g15)
    c: Coincident(g63,g8)
    c: Equal(g61,g62)
    c: Equal(g62,g63)
    c: Equal(g63,g58)
    c: Equal(g58,g59)
    c: Equal(g59,g60)
    c: Equal(g60,g55)
    c: Equal(g55,g56)
    c: Equal(g56,g57)
    c: Equal(g57,g54)
    c: Equal(g54,g53)
    c: Equal(g53,g52)
    c: Equal(g52,g51)
    c: Equal(g51,g50)
    c: Equal(g50,g49)
    c: Equal(g49,g46)
    c: Equal(g46,g47)
    c: Equal(g47,g48)
    c: Radius(g55) = 0.75
FEATURE [Sketcher::SketchObject] Sketch1257
  MapMode = 5
  Support = -> [XY_Plane540]
FEATURE [Sketcher::SketchObject] Sketch1258
  MapMode = 5
  Support = -> [XY_Plane437]
  sketch-geometry (1):
    g0: Circle CenterX=0 CenterY=0 CenterZ=0 NormalX=0 NormalY=0 NormalZ=1 AngleXU=0 Radius=1.9
  constraints (2):
    c: Coincident(g0,g-1)
    c: Radius(g0) = 1.9
FEATURE [Sketcher::SketchObject] Sketch1259
  MapMode = 5
  Support = -> [XY_Plane452]
  sketch-geometry (8):
    g0: LineSegment StartX=0 StartY=2.3094 StartZ=0 EndX=-2 EndY=1.1547 EndZ=0
    g1: LineSegment StartX=-2 StartY=1.1547 StartZ=0 EndX=-2 EndY=-1.1547 EndZ=0
    g2: LineSegment StartX=-2 StartY=-1.1547 StartZ=0 EndX=-2e-16 EndY=-2.3094 EndZ=0
    g3: LineSegment StartX=-2e-16 StartY=-2.3094 StartZ=0 EndX=2 EndY=-1.1547 EndZ=0
    g4: LineSegment StartX=2 StartY=-1.1547 StartZ=0 EndX=2 EndY=1.1547 EndZ=0
    g5: LineSegment StartX=2 StartY=1.1547 StartZ=0 EndX=0 EndY=2.3094 EndZ=0
    g6: Circle [constr] CenterX=0 CenterY=0 CenterZ=0 NormalX=0 NormalY=0 NormalZ=1 AngleXU=0 Radius=2.3094
    g7: Circle CenterX=0 CenterY=0 CenterZ=0 NormalX=0 NormalY=0 NormalZ=1 AngleXU=0 Radius=1
  constraints (18):
    c: Coincident(g0,g1)
    c: Coincident(g1,g2)
    c: Coincident(g2,g3)
    c: Coincident(g3,g4)
    c: Coincident(g4,g5)
    c: Coincident(g5,g0)
    c: Equal(g0, g1-g5) x5
    c: PointOnObject(g0,g6)
    c: PointOnObject(g1,g6)
    c: PointOnObject(g2,g6)
    c: PointOnObject(g3,g6)
    c: PointOnObject(g4,g6)
    c: PointOnObject(g5,g6)
    c: Coincident(g6,g-1)
    c: PointOnObject(g5,g-2)
    c: DistanceX(g0,g4) = 4
    c: Coincident(g7,g-1)
    c: Radius(g7) = 1
FEATURE [Sketcher::SketchObject] Sketch1262
  MapMode = 5
  Support = -> [XY_Plane424]
  sketch-geometry (1):
    g0: Circle CenterX=0 CenterY=0 CenterZ=0 NormalX=0 NormalY=0 NormalZ=1 AngleXU=0 Radius=2.75
  constraints (2):
    c: Coincident(g0,g-1)
    c: Radius(g0) = 2.75
FEATURE [Sketcher::SketchObject] Sketch1267
  MapMode = 5
  Support = -> [XY_Plane432]
  sketch-geometry (8):
    g0: LineSegment StartX=0 StartY=3.17543 StartZ=0 EndX=-2.75 EndY=1.58771 EndZ=0
    g1: LineSegment StartX=-2.75 StartY=1.58771 StartZ=0 EndX=-2.75 EndY=-1.58771 EndZ=0
    g2: LineSegment StartX=-2.75 StartY=-1.58771 StartZ=0 EndX=0 EndY=-3.17543 EndZ=0
    g3: LineSegment StartX=0 StartY=-3.17543 StartZ=0 EndX=2.75 EndY=-1.58771 EndZ=0
    g4: LineSegment StartX=2.75 StartY=-1.58771 StartZ=0 EndX=2.75 EndY=1.58771 EndZ=0
    g5: LineSegment StartX=2.75 StartY=1.58771 StartZ=0 EndX=0 EndY=3.17543 EndZ=0
    g6: Circle [constr] CenterX=0 CenterY=0 CenterZ=0 NormalX=0 NormalY=0 NormalZ=1 AngleXU=0 Radius=3.17543
    g7: Circle CenterX=0 CenterY=0 CenterZ=0 NormalX=0 NormalY=0 NormalZ=1 AngleXU=0 Radius=1.5
  constraints (18):
    c: Coincident(g0,g1)
    c: Coincident(g1,g2)
    c: Coincident(g2,g3)
    c: Coincident(g3,g4)
    c: Coincident(g4,g5)
    c: Coincident(g5,g0)
    c: Equal(g0, g1-g5) x5
    c: PointOnObject(g0,g6)
    c: PointOnObject(g1,g6)
    c: PointOnObject(g2,g6)
    c: PointOnObject(g3,g6)
    c: PointOnObject(g4,g6)
    c: PointOnObject(g5,g6)
    c: Coincident(g6,g-1)
    c: PointOnObject(g5,g-2)
    c: DistanceX(g0,g4) = 5.5
    c: Coincident(g7,g-1)
    c: Radius(g7) = 1.5
FEATURE [Sketcher::SketchObject] Sketch1269
  MapMode = 5
  Support = -> [XY_Plane433]
  sketch-geometry (8):
    g0: LineSegment StartX=0 StartY=3.17543 StartZ=0 EndX=-2.75 EndY=1.58771 EndZ=0
    g1: LineSegment StartX=-2.75 StartY=1.58771 StartZ=0 EndX=-2.75 EndY=-1.58771 EndZ=0
    g2: LineSegment StartX=-2.75 StartY=-1.58771 StartZ=0 EndX=0 EndY=-3.17543 EndZ=0
    g3: LineSegment StartX=0 StartY=-3.17543 StartZ=0 EndX=2.75 EndY=-1.58771 EndZ=0
    g4: LineSegment StartX=2.75 StartY=-1.58771 StartZ=0 EndX=2.75 EndY=1.58771 EndZ=0
    g5: LineSegment StartX=2.75 StartY=1.58771 StartZ=0 EndX=0 EndY=3.17543 EndZ=0
    g6: Circle [constr] CenterX=0 CenterY=0 CenterZ=0 NormalX=0 NormalY=0 NormalZ=1 AngleXU=0 Radius=3.17543
    g7: Circle CenterX=0 CenterY=0 CenterZ=0 NormalX=0 NormalY=0 NormalZ=1 AngleXU=0 Radius=1.5
  constraints (18):
    c: Coincident(g0,g1)
    c: Coincident(g1,g2)
    c: Coincident(g2,g3)
    c: Coincident(g3,g4)
    c: Coincident(g4,g5)
    c: Coincident(g5,g0)
    c: Equal(g0, g1-g5) x5
    c: PointOnObject(g0,g6)
    c: PointOnObject(g1,g6)
    c: PointOnObject(g2,g6)
    c: PointOnObject(g3,g6)
    c: PointOnObject(g4,g6)
    c: PointOnObject(g5,g6)
    c: Coincident(g6,g-1)
    c: PointOnObject(g5,g-2)
    c: DistanceX(g0,g4) = 5.5
    c: Coincident(g7,g-1)
    c: Radius(g7) = 1.5
FEATURE [Sketcher::SketchObject] Sketch1270
  MapMode = 5
  Support = -> [XY_Plane423]
  sketch-geometry (8):
    g0: LineSegment StartX=0 StartY=3.17543 StartZ=0 EndX=-2.75 EndY=1.58771 EndZ=0
    g1: LineSegment StartX=-2.75 StartY=1.58771 StartZ=0 EndX=-2.75 EndY=-1.58771 EndZ=0
    g2: LineSegment StartX=-2.75 StartY=-1.58771 StartZ=0 EndX=0 EndY=-3.17543 EndZ=0
    g3: LineSegment StartX=0 StartY=-3.17543 StartZ=0 EndX=2.75 EndY=-1.58771 EndZ=0
    g4: LineSegment StartX=2.75 StartY=-1.58771 StartZ=0 EndX=2.75 EndY=1.58771 EndZ=0
    g5: LineSegment StartX=2.75 StartY=1.58771 StartZ=0 EndX=0 EndY=3.17543 EndZ=0
    g6: Circle [constr] CenterX=0 CenterY=0 CenterZ=0 NormalX=0 NormalY=0 NormalZ=1 AngleXU=0 Radius=3.17543
    g7: Circle CenterX=0 CenterY=0 CenterZ=0 NormalX=0 NormalY=0 NormalZ=1 AngleXU=0 Radius=1.5
  constraints (18):
    c: Coincident(g0,g1)
    c: Coincident(g1,g2)
    c: Coincident(g2,g3)
    c: Coincident(g3,g4)
    c: Coincident(g4,g5)
    c: Coincident(g5,g0)
    c: Equal(g0, g1-g5) x5
    c: PointOnObject(g0,g6)
    c: PointOnObject(g1,g6)
    c: PointOnObject(g2,g6)
    c: PointOnObject(g3,g6)
    c: PointOnObject(g4,g6)
    c: PointOnObject(g5,g6)
    c: Coincident(g6,g-1)
    c: PointOnObject(g5,g-2)
    c: DistanceX(g0,g4) = 5.5
    c: Coincident(g7,g-1)
    c: Radius(g7) = 1.5
FEATURE [Sketcher::SketchObject] Sketch1271
  MapMode = 5
  Support = -> [XY_Plane531]
FEATURE [Sketcher::SketchObject] Sketch1276
  MapMode = 5
  Support = -> [XY_Plane468]
  sketch-geometry (1):
    g0: Circle CenterX=0 CenterY=0 CenterZ=0 NormalX=0 NormalY=0 NormalZ=1 AngleXU=0 Radius=2.75
  constraints (2):
    c: Coincident(g0,g-1)
    c: Radius(g0) = 2.75
FEATURE [Sketcher::SketchObject] Sketch1277
  MapMode = 5
  Support = -> [XY_Plane482]
  sketch-geometry (4):
    g0: LineSegment StartX=0 StartY=0 StartZ=0 EndX=56.5 EndY=0 EndZ=0
    g1: LineSegment StartX=56.5 StartY=0 StartZ=0 EndX=56.5 EndY=-22 EndZ=0
    g2: LineSegment StartX=56.5 StartY=-22 StartZ=0 EndX=0 EndY=-22 EndZ=0
    g3: LineSegment StartX=0 StartY=-22 StartZ=0 EndX=0 EndY=0 EndZ=0
  constraints (11):
    c: Coincident(g0,g1)
    c: Coincident(g1,g2)
    c: Coincident(g2,g3)
    c: Coincident(g3,g0)
    c: Horizontal(g0)
    c: Horizontal(g2)
    c: Vertical(g1)
    c: Vertical(g3)
    c: Coincident(g0,g-1)
    c: DistanceX(g2,g2) = 56.5
    c: DistanceY(g3,g3) = 22
FEATURE [Sketcher::SketchObject] Sketch1278
  MapMode = 5
  Support = -> [XY_Plane474]
  sketch-geometry (8):
    g0: LineSegment StartX=-20 StartY=14 StartZ=0 EndX=20 EndY=14 EndZ=0
    g1: LineSegment StartX=20 StartY=14 StartZ=0 EndX=20 EndY=19 EndZ=0
    g2: LineSegment StartX=20 StartY=19 StartZ=0 EndX=-20 EndY=19 EndZ=0
    g3: LineSegment StartX=-20 StartY=19 StartZ=0 EndX=-20 EndY=14 EndZ=0
    g4: LineSegment StartX=-20 StartY=-19 StartZ=0 EndX=20 EndY=-19 EndZ=0
    g5: LineSegment StartX=20 StartY=-19 StartZ=0 EndX=20 EndY=-14 EndZ=0
    g6: LineSegment StartX=20 StartY=-14 StartZ=0 EndX=-20 EndY=-14 EndZ=0
    g7: LineSegment StartX=-20 StartY=-14 StartZ=0 EndX=-20 EndY=-19 EndZ=0
  constraints (22):
    c: Coincident(g0,g1)
    c: Coincident(g1,g2)
    c: Coincident(g2,g3)
    c: Coincident(g3,g0)
    c: Horizontal(g0)
    c: Vertical(g1)
    c: Vertical(g3)
    c: Coincident(g4,g5)
    c: Coincident(g5,g6)
    c: Coincident(g6,g7)
    c: Coincident(g7,g4)
    c: Horizontal(g4)
    c: Horizontal(g6)
    c: Vertical(g5)
    c: Vertical(g7)
    c: Equal(g1,g5)
    c: Equal(g6,g2)
    c: Symmetric(g1,g2,g-2)
    c: Symmetric(g1,g4,g-1)
    c: DistanceY(g1,g1) = 5
    c: DistanceY(g5,g0) = 28
    c: DistanceX(g2,g2) = 40
FEATURE [Sketcher::SketchObject] Sketch1284
  MapMode = 5
  Support = -> [XY_Plane489]
  sketch-geometry (8):
    g0: LineSegment StartX=0 StartY=3.17543 StartZ=0 EndX=-2.75 EndY=1.58771 EndZ=0
    g1: LineSegment StartX=-2.75 StartY=1.58771 StartZ=0 EndX=-2.75 EndY=-1.58771 EndZ=0
    g2: LineSegment StartX=-2.75 StartY=-1.58771 StartZ=0 EndX=0 EndY=-3.17543 EndZ=0
    g3: LineSegment StartX=0 StartY=-3.17543 StartZ=0 EndX=2.75 EndY=-1.58771 EndZ=0
    g4: LineSegment StartX=2.75 StartY=-1.58771 StartZ=0 EndX=2.75 EndY=1.58771 EndZ=0
    g5: LineSegment StartX=2.75 StartY=1.58771 StartZ=0 EndX=0 EndY=3.17543 EndZ=0
    g6: Circle [constr] CenterX=0 CenterY=0 CenterZ=0 NormalX=0 NormalY=0 NormalZ=1 AngleXU=0 Radius=3.17543
    g7: Circle CenterX=0 CenterY=0 CenterZ=0 NormalX=0 NormalY=0 NormalZ=1 AngleXU=0 Radius=1.5
  constraints (18):
    c: Coincident(g0,g1)
    c: Coincident(g1,g2)
    c: Coincident(g2,g3)
    c: Coincident(g3,g4)
    c: Coincident(g4,g5)
    c: Coincident(g5,g0)
    c: Equal(g0, g1-g5) x5
    c: PointOnObject(g0,g6)
    c: PointOnObject(g1,g6)
    c: PointOnObject(g2,g6)
    c: PointOnObject(g3,g6)
    c: PointOnObject(g4,g6)
    c: PointOnObject(g5,g6)
    c: Coincident(g6,g-1)
    c: PointOnObject(g5,g-2)
    c: DistanceX(g0,g4) = 5.5
    c: Coincident(g7,g-1)
    c: Radius(g7) = 1.5
FEATURE [Sketcher::SketchObject] Sketch1285
  MapMode = 5
  Support = -> [XY_Plane486]
  sketch-geometry (8):
    g0: LineSegment StartX=0 StartY=3.17543 StartZ=0 EndX=-2.75 EndY=1.58771 EndZ=0
    g1: LineSegment StartX=-2.75 StartY=1.58771 StartZ=0 EndX=-2.75 EndY=-1.58771 EndZ=0
    g2: LineSegment StartX=-2.75 StartY=-1.58771 StartZ=0 EndX=0 EndY=-3.17543 EndZ=0
    g3: LineSegment StartX=0 StartY=-3.17543 StartZ=0 EndX=2.75 EndY=-1.58771 EndZ=0
    g4: LineSegment StartX=2.75 StartY=-1.58771 StartZ=0 EndX=2.75 EndY=1.58771 EndZ=0
    g5: LineSegment StartX=2.75 StartY=1.58771 StartZ=0 EndX=0 EndY=3.17543 EndZ=0
    g6: Circle [constr] CenterX=0 CenterY=0 CenterZ=0 NormalX=0 NormalY=0 NormalZ=1 AngleXU=0 Radius=3.17543
    g7: Circle CenterX=0 CenterY=0 CenterZ=0 NormalX=0 NormalY=0 NormalZ=1 AngleXU=0 Radius=1.5
  constraints (18):
    c: Coincident(g0,g1)
    c: Coincident(g1,g2)
    c: Coincident(g2,g3)
    c: Coincident(g3,g4)
    c: Coincident(g4,g5)
    c: Coincident(g5,g0)
    c: Equal(g0, g1-g5) x5
    c: PointOnObject(g0,g6)
    c: PointOnObject(g1,g6)
    c: PointOnObject(g2,g6)
    c: PointOnObject(g3,g6)
    c: PointOnObject(g4,g6)
    c: PointOnObject(g5,g6)
    c: Coincident(g6,g-1)
    c: PointOnObject(g5,g-2)
    c: DistanceX(g0,g4) = 5.5
    c: Coincident(g7,g-1)
    c: Radius(g7) = 1.5
FEATURE [Sketcher::SketchObject] Sketch1290
  MapMode = 5
  Placement = pos=(0,0,0) rot=(0.57735,0.57735,0.57735;2.0944rad)
  Support = -> [YZ_Plane493]
  sketch-geometry (4):
    g0: LineSegment StartX=35.5 StartY=12.9 StartZ=0 EndX=38.5 EndY=12.9 EndZ=0
    g1: LineSegment StartX=38.5 StartY=12.9 StartZ=0 EndX=38.5 EndY=7.1 EndZ=0
    g2: LineSegment StartX=38.5 StartY=7.1 StartZ=0 EndX=35.5 EndY=7.1 EndZ=0
    g3: LineSegment StartX=35.5 StartY=7.1 StartZ=0 EndX=35.5 EndY=12.9 EndZ=0
  constraints (12):
    c: Coincident(g0,g1)
    c: Coincident(g1,g2)
    c: Coincident(g2,g3)
    c: Coincident(g3,g0)
    c: Horizontal(g0)
    c: Horizontal(g2)
    c: Vertical(g1)
    c: Vertical(g3)
    c: DistanceY(g-1,g1) = 7.1
    c: DistanceY(g3,g3) = 5.8
    c: DistanceX(g0,g0) = 3
    c: DistanceX(g-1,g1) = 38.5
FEATURE [Sketcher::SketchObject] Sketch1291
  MapMode = 5
  Support = -> [XY_Plane480]
  sketch-geometry (8):
    g0: LineSegment StartX=0 StartY=2.3094 StartZ=0 EndX=-2 EndY=1.1547 EndZ=0
    g1: LineSegment StartX=-2 StartY=1.1547 StartZ=0 EndX=-2 EndY=-1.1547 EndZ=0
    g2: LineSegment StartX=-2 StartY=-1.1547 StartZ=0 EndX=-2e-16 EndY=-2.3094 EndZ=0
    g3: LineSegment StartX=-2e-16 StartY=-2.3094 StartZ=0 EndX=2 EndY=-1.1547 EndZ=0
    g4: LineSegment StartX=2 StartY=-1.1547 StartZ=0 EndX=2 EndY=1.1547 EndZ=0
    g5: LineSegment StartX=2 StartY=1.1547 StartZ=0 EndX=0 EndY=2.3094 EndZ=0
    g6: Circle [constr] CenterX=0 CenterY=0 CenterZ=0 NormalX=0 NormalY=0 NormalZ=1 AngleXU=0 Radius=2.3094
    g7: Circle CenterX=0 CenterY=0 CenterZ=0 NormalX=0 NormalY=0 NormalZ=1 AngleXU=0 Radius=1
  constraints (18):
    c: Coincident(g0,g1)
    c: Coincident(g1,g2)
    c: Coincident(g2,g3)
    c: Coincident(g3,g4)
    c: Coincident(g4,g5)
    c: Coincident(g5,g0)
    c: Equal(g0, g1-g5) x5
    c: PointOnObject(g0,g6)
    c: PointOnObject(g1,g6)
    c: PointOnObject(g2,g6)
    c: PointOnObject(g3,g6)
    c: PointOnObject(g4,g6)
    c: PointOnObject(g5,g6)
    c: Coincident(g6,g-1)
    c: PointOnObject(g5,g-2)
    c: DistanceX(g0,g4) = 4
    c: Coincident(g7,g-1)
    c: Radius(g7) = 1
FEATURE [Sketcher::SketchObject] Sketch1293
  MapMode = 5
  Support = -> [XY_Plane481]
  sketch-geometry (8):
    g0: LineSegment StartX=0 StartY=3.17543 StartZ=0 EndX=-2.75 EndY=1.58771 EndZ=0
    g1: LineSegment StartX=-2.75 StartY=1.58771 StartZ=0 EndX=-2.75 EndY=-1.58771 EndZ=0
    g2: LineSegment StartX=-2.75 StartY=-1.58771 StartZ=0 EndX=0 EndY=-3.17543 EndZ=0
    g3: LineSegment StartX=0 StartY=-3.17543 StartZ=0 EndX=2.75 EndY=-1.58771 EndZ=0
    g4: LineSegment StartX=2.75 StartY=-1.58771 StartZ=0 EndX=2.75 EndY=1.58771 EndZ=0
    g5: LineSegment StartX=2.75 StartY=1.58771 StartZ=0 EndX=0 EndY=3.17543 EndZ=0
    g6: Circle [constr] CenterX=0 CenterY=0 CenterZ=0 NormalX=0 NormalY=0 NormalZ=1 AngleXU=0 Radius=3.17543
    g7: Circle CenterX=0 CenterY=0 CenterZ=0 NormalX=0 NormalY=0 NormalZ=1 AngleXU=0 Radius=1.5
  constraints (18):
    c: Coincident(g0,g1)
    c: Coincident(g1,g2)
    c: Coincident(g2,g3)
    c: Coincident(g3,g4)
    c: Coincident(g4,g5)
    c: Coincident(g5,g0)
    c: Equal(g0, g1-g5) x5
    c: PointOnObject(g0,g6)
    c: PointOnObject(g1,g6)
    c: PointOnObject(g2,g6)
    c: PointOnObject(g3,g6)
    c: PointOnObject(g4,g6)
    c: PointOnObject(g5,g6)
    c: Coincident(g6,g-1)
    c: PointOnObject(g5,g-2)
    c: DistanceX(g0,g4) = 5.5
    c: Coincident(g7,g-1)
    c: Radius(g7) = 1.5
FEATURE [Sketcher::SketchObject] Sketch1298
  MapMode = 5
  Placement = pos=(0,0,0) rot=(1,0,0;1.5708rad)
  Support = -> [XZ_Plane567]
  sketch-geometry (1):
    g0: Circle CenterX=-1.55 CenterY=4 CenterZ=0 NormalX=0 NormalY=0 NormalZ=1 AngleXU=0 Radius=0.75
  constraints (3):
    c: Radius(g0) = 0.75
    c: DistanceY(g-1,g0) = 4
    c: DistanceX(g0,g-1) = 1.55
FEATURE [Sketcher::SketchObject] Sketch1305
  MapMode = 5
  Support = -> [XY_Plane490]
  sketch-geometry (12):
    g0: LineSegment StartX=0 StartY=0 StartZ=0 EndX=0 EndY=57 EndZ=0
    g1: LineSegment StartX=0 StartY=57 StartZ=0 EndX=40 EndY=57 EndZ=0
    g2: ArcOfCircle CenterX=40 CenterY=44.5 CenterZ=0 NormalX=0 NormalY=0 NormalZ=1 AngleXU=0 Radius=12.5 StartAngle=0.643501 EndAngle=1.5708
    g3: ArcOfCircle CenterX=60 CenterY=59.5 CenterZ=0 NormalX=0 NormalY=0 NormalZ=1 AngleXU=0 Radius=12.5 StartAngle=3.78509 EndAngle=4.71239
    g4: LineSegment StartX=60 StartY=47 StartZ=0 EndX=120 EndY=47 EndZ=0
    g5: ArcOfCircle CenterX=120 CenterY=37 CenterZ=0 NormalX=0 NormalY=0 NormalZ=1 AngleXU=0 Radius=10 StartAngle=2e-16 EndAngle=1.5708
    g6: LineSegment StartX=130 StartY=37 StartZ=0 EndX=130 EndY=15 EndZ=0
    g7: ArcOfCircle CenterX=125 CenterY=15 CenterZ=0 NormalX=0 NormalY=0 NormalZ=1 AngleXU=0 Radius=5 StartAngle=4.71239 EndAngle=6.28319
    g8: LineSegment StartX=125 StartY=10 StartZ=0 EndX=60 EndY=10 EndZ=0
    g9: LineSegment StartX=40 StartY=0 StartZ=0 EndX=0 EndY=0 EndZ=0
    g10: ArcOfCircle CenterX=40 CenterY=12.5 CenterZ=0 NormalX=0 NormalY=0 NormalZ=1 AngleXU=0 Radius=12.5 StartAngle=4.71239 EndAngle=5.63968
    g11: ArcOfCircle CenterX=60 CenterY=-2.5 CenterZ=0 NormalX=0 NormalY=0 NormalZ=1 AngleXU=0 Radius=12.5 StartAngle=1.5708 EndAngle=2.49809
  constraints (31):
    c: Coincident(g-1,g0)
    c: PointOnObject(g0,g-2)
    c: Coincident(g0,g1)
    c: Horizontal(g1)
    c: Tangent(g1,g2) = 1.5708
    c: Tangent(g2,g3) = 1.5708
    c: Tangent(g3,g4) = -1.5708
    c: Tangent(g4,g5) = 1.5708
    c: Tangent(g5,g6) = 1.5708
    c: Tangent(g6,g7) = 1.5708
    c: Tangent(g7,g8) = 1.5708
    c: Coincident(g9,g0)
    c: Horizontal(g9)
    c: Horizontal(g4)
    c: Horizontal(g8)
    c: Vertical(g6)
    c: Tangent(g11,g8) = -1.5708
    c: Tangent(g11,g10) = 1.5708
    c: Radius(g7) = 5
    c: Radius(g5) = 10
    c: DistanceX(g1,g1) = 40
    c: DistanceX(g0,g6) = 130
    c: DistanceX(g1,g3) = 20
    c: Tangent(g10,g9) = 1.5708
    c: DistanceX(g9,g8) = 20
    c: DistanceX(g9,g9) = 40
    c: DistanceY(g0,g0) = 57
    c: DistanceY(g9,g8) = 10
    c: DistanceY(g3,g1) = 10
    c: DistanceX(g10,g8) = 10
    c: DistanceX(g2,g3) = 10
FEATURE [PartDesign::Pad] Pad477  label="Baseplate021"
  Length = 30
  Length2 = 100
  Profile = -> Sketch1305
  Type = 0
FEATURE [PartDesign::Pocket] Pocket433  label="Servohorn Mount Pocket004"
  BaseFeature = -> Pad477
  Length = 5
  Length2 = 100
  Profile = -> Pad477 [Face12]
  Type = 0
FEATURE [Sketcher::SketchObject] Sketch1306
  MapMode = 5
  Support = -> [XY_Plane545]
  sketch-geometry (9):
    g0: ArcOfCircle CenterX=0 CenterY=0 CenterZ=0 NormalX=0 NormalY=0 NormalZ=1 AngleXU=0 Radius=16.5 StartAngle=3.66519 EndAngle=6.80678
    g1: LineSegment StartX=-14.2894 StartY=-8.25 StartZ=0 EndX=-27.2211 EndY=14.1484 EndZ=0
    g2: LineSegment StartX=1.3577 StartY=30.6484 StartZ=0 EndX=14.2894 EndY=8.25 EndZ=0
    g3: LineSegment [constr] StartX=-27.2211 StartY=14.1484 StartZ=0 EndX=1.3577 EndY=30.6484 EndZ=0
    g4: ArcOfCircle CenterX=-28.6962 CenterY=13.2968 CenterZ=0 NormalX=0 NormalY=0 NormalZ=1 AngleXU=0 Radius=1.70319 StartAngle=0.523599 EndAngle=1.5708
    g5: ArcOfCircle CenterX=-23.5 CenterY=16.2968 CenterZ=0 NormalX=0 NormalY=0 NormalZ=1 AngleXU=0 Radius=28.7032 StartAngle=0.523599 EndAngle=1.5708
    g6: LineSegment StartX=-28.6962 StartY=15 StartZ=0 EndX=-40 EndY=15 EndZ=0
    g7: LineSegment StartX=-40 StartY=15 StartZ=0 EndX=-40 EndY=45 EndZ=0
    g8: LineSegment StartX=-40 StartY=45 StartZ=0 EndX=-23.5 EndY=45 EndZ=0
  constraints (22):
    c: Coincident(g0,g-1)
    c: Tangent(g0,g1) = 1.5708
    c: Coincident(g3,g2) = -1.5708
    c: Parallel(g2,g1)
    c: Radius(g0) = 16.5
    c: Tangent(g2,g0) = 1.5708
    c: Coincident(g3,g1)
    c: Perpendicular(g1,g3)
    c: Tangent(g5,g2) = 1.5708
    c: Tangent(g4,g1) = -1.5708
    c: Horizontal(g6)
    c: Coincident(g7,g6)
    c: Vertical(g7)
    c: Coincident(g8,g7)
    c: Horizontal(g8)
    c: Tangent(g6,g4) = -1.5708
    c: DistanceY(g7,g7) = 30
    c: DistanceX(g6,g0) = 40
    c: DistanceX(g8,g8) = 16.5
    c: Tangent(g8,g5) = 1.5708
    c: DistanceY(g0,g4) = 15
    c: Angle(g3) = 0.523599
FEATURE [Sketcher::SketchObject] Sketch1308
  MapMode = 5
  Support = -> [XY_Plane561]
  sketch-geometry (1):
    g0: Circle CenterX=0 CenterY=0 CenterZ=0 NormalX=0 NormalY=0 NormalZ=1 AngleXU=0 Radius=1.9
  constraints (2):
    c: Coincident(g0,g-1)
    c: Radius(g0) = 1.9
FEATURE [Sketcher::SketchObject] Sketch1309
  MapMode = 5
  Support = -> [XY_Plane543]
FEATURE [Sketcher::SketchObject] Sketch1310
  MapMode = 5
  Support = -> [XY_Plane559]
FEATURE [Sketcher::SketchObject] Sketch1311
  MapMode = 5
  Support = -> [XY_Plane559]
FEATURE [Sketcher::SketchObject] Sketch1315
  MapMode = 5
  Placement = pos=(0,0,0) rot=(1,0,0;1.5708rad)
  Support = -> [XZ_Plane478]
  sketch-geometry (1):
    g0: Circle CenterX=0 CenterY=4 CenterZ=0 NormalX=0 NormalY=0 NormalZ=1 AngleXU=0 Radius=0.75
  constraints (3):
    c: PointOnObject(g0,g-2)
    c: Radius(g0) = 0.75
    c: DistanceY(g-1,g0) = 4
FEATURE [PartDesign::Pad] Pad479
  Length = 10
  Length2 = 100
  Placement = pos=(0,0,0) rot=(1,0,0;1.5708rad)
  Profile = -> Sketch1315
  Reversed = true
  Type = 0
FEATURE [PartDesign::Body] Body303  label="red wire009"
  Group = -> [Sketch1315,Pad479]
  Origin = -> Origin459
  Placement = pos=(0,25.15,0) rot=(0,0,1;0rad)
  Tip = -> Pad479
FEATURE [Sketcher::SketchObject] Sketch1317
  MapMode = 5
  Support = -> [XY_Plane478]
  sketch-geometry (8):
    g0: LineSegment StartX=0 StartY=3.17543 StartZ=0 EndX=-2.75 EndY=1.58771 EndZ=0
    g1: LineSegment StartX=-2.75 StartY=1.58771 StartZ=0 EndX=-2.75 EndY=-1.58771 EndZ=0
    g2: LineSegment StartX=-2.75 StartY=-1.58771 StartZ=0 EndX=0 EndY=-3.17543 EndZ=0
    g3: LineSegment StartX=0 StartY=-3.17543 StartZ=0 EndX=2.75 EndY=-1.58771 EndZ=0
    g4: LineSegment StartX=2.75 StartY=-1.58771 StartZ=0 EndX=2.75 EndY=1.58771 EndZ=0
    g5: LineSegment StartX=2.75 StartY=1.58771 StartZ=0 EndX=0 EndY=3.17543 EndZ=0
    g6: Circle [constr] CenterX=0 CenterY=0 CenterZ=0 NormalX=0 NormalY=0 NormalZ=1 AngleXU=0 Radius=3.17543
    g7: Circle CenterX=0 CenterY=0 CenterZ=0 NormalX=0 NormalY=0 NormalZ=1 AngleXU=0 Radius=1.5
  constraints (18):
    c: Coincident(g0,g1)
    c: Coincident(g1,g2)
    c: Coincident(g2,g3)
    c: Coincident(g3,g4)
    c: Coincident(g4,g5)
    c: Coincident(g5,g0)
    c: Equal(g0, g1-g5) x5
    c: PointOnObject(g0,g6)
    c: PointOnObject(g1,g6)
    c: PointOnObject(g2,g6)
    c: PointOnObject(g3,g6)
    c: PointOnObject(g4,g6)
    c: PointOnObject(g5,g6)
    c: Coincident(g6,g-1)
    c: PointOnObject(g5,g-2)
    c: DistanceX(g0,g4) = 5.5
    c: Coincident(g7,g-1)
    c: Radius(g7) = 1.5
FEATURE [Sketcher::SketchObject] Sketch1318
  MapMode = 5
  Support = -> [XY_Plane477]
  sketch-geometry (1):
    g0: Circle CenterX=0 CenterY=0 CenterZ=0 NormalX=0 NormalY=0 NormalZ=1 AngleXU=0 Radius=2.75
  constraints (2):
    c: Coincident(g0,g-1)
    c: Radius(g0) = 2.75
FEATURE [Sketcher::SketchObject] Sketch1321
  MapMode = 5
  Support = -> [XY_Plane551]
  sketch-geometry (1):
    g0: Circle CenterX=0 CenterY=0 CenterZ=0 NormalX=0 NormalY=0 NormalZ=1 AngleXU=0 Radius=2.75
  constraints (2):
    c: Coincident(g0,g-1)
    c: Radius(g0) = 2.75
FEATURE [Sketcher::SketchObject] Sketch1322
  MapMode = 5
  Support = -> [XY_Plane552]
  sketch-geometry (1):
    g0: Circle CenterX=0 CenterY=10.15 CenterZ=0 NormalX=0 NormalY=0 NormalZ=1 AngleXU=0 Radius=3
  constraints (3):
    c: PointOnObject(g0,g-2)
    c: DistanceY(g-1,g0) = 10.15
    c: Radius(g0) = 3
FEATURE [PartDesign::Pad] Pad476
  Length = 5
  Length2 = 100
  Profile = -> Sketch1322
  Type = 0
FEATURE [Sketcher::SketchObject] Sketch1314
  ExternalGeometry = -> [Pad476]
  MapMode = 5
  Placement = pos=(0,0,5) rot=(0,0,1;0rad)
  Support = -> [Pad476]
  sketch-geometry (1):
    g0: Circle CenterX=0 CenterY=10.15 CenterZ=0 NormalX=0 NormalY=0 NormalZ=1 AngleXU=0 Radius=1.5
  constraints (2):
    c: Coincident(g0,g-3)
    c: Radius(g0) = 1.5
FEATURE [Sketcher::SketchObject] Sketch1324
  MapMode = 5
  Support = -> [XY_Plane494]
  sketch-geometry (1):
    g0: Circle CenterX=0 CenterY=0 CenterZ=0 NormalX=0 NormalY=0 NormalZ=1 AngleXU=0 Radius=2.75
  constraints (2):
    c: Coincident(g0,g-1)
    c: Radius(g0) = 2.75
FEATURE [Sketcher::SketchObject] Sketch1329
  MapMode = 5
  Placement = pos=(0,0,0) rot=(1,0,0;1.5708rad)
  Support = -> [XZ_Plane553]
  sketch-geometry (1):
    g0: Circle CenterX=1.55 CenterY=4 CenterZ=0 NormalX=0 NormalY=0 NormalZ=1 AngleXU=0 Radius=0.75
  constraints (3):
    c: Radius(g0) = 0.75
    c: DistanceY(g-1,g0) = 4
    c: DistanceX(g-1,g0) = 1.55
FEATURE [PartDesign::Pad] Pad484
  Length = 10
  Length2 = 100
  Placement = pos=(0,0,0) rot=(1,0,0;1.5708rad)
  Profile = -> Sketch1329
  Reversed = true
  Type = 0
FEATURE [PartDesign::Body] Body340  label="brown wire010"
  Group = -> [Sketch1329,Pad484]
  Origin = -> Origin505
  Placement = pos=(0,25.15,0) rot=(0,0,1;0rad)
  Tip = -> Pad484
FEATURE [Sketcher::SketchObject] Sketch1331
  MapMode = 5
  Support = -> [XY_Plane469]
  sketch-geometry (2):
    g0: Circle CenterX=0 CenterY=0 CenterZ=0 NormalX=0 NormalY=0 NormalZ=1 AngleXU=0 Radius=2.5
    g1: Circle CenterX=0 CenterY=0 CenterZ=0 NormalX=0 NormalY=0 NormalZ=1 AngleXU=0 Radius=1
  constraints (4):
    c: Coincident(g0,g-1)
    c: Coincident(g1,g0)
    c: Radius(g0) = 2.5
    c: Radius(g1) = 1
FEATURE [Sketcher::SketchObject] Sketch1337
  MapMode = 5
  Support = -> [XY_Plane484]
  sketch-geometry (9):
    g0: LineSegment StartX=-2.8e-15 StartY=0 StartZ=0 EndX=56.5 EndY=0 EndZ=0
    g1: LineSegment StartX=56.5 StartY=0 StartZ=0 EndX=56.5 EndY=25 EndZ=0
    g2: LineSegment StartX=51.5 StartY=30 StartZ=0 EndX=-80 EndY=30 EndZ=0
    g3: ArcOfCircle CenterX=-80 CenterY=15 CenterZ=0 NormalX=0 NormalY=0 NormalZ=1 AngleXU=0 Radius=15 StartAngle=1.5708 EndAngle=5.50197
    g4: ArcOfCircle CenterX=-50 CenterY=-14.75 CenterZ=0 NormalX=0 NormalY=0 NormalZ=1 AngleXU=0 Radius=27.25 StartAngle=1.5708 EndAngle=2.36038
    g5: ArcOfCircle CenterX=-30 CenterY=-14.75 CenterZ=0 NormalX=0 NormalY=0 NormalZ=1 AngleXU=0 Radius=27.25 StartAngle=0.781214 EndAngle=1.5708
    g6: ArcOfCircle CenterX=0 CenterY=15 CenterZ=0 NormalX=0 NormalY=0 NormalZ=1 AngleXU=0 Radius=15 StartAngle=3.92281 EndAngle=4.71239
    g7: LineSegment StartX=-50 StartY=12.5 StartZ=0 EndX=-30 EndY=12.5 EndZ=0
    g8: ArcOfCircle CenterX=51.5 CenterY=25 CenterZ=0 NormalX=0 NormalY=0 NormalZ=1 AngleXU=0 Radius=5 StartAngle=3e-16 EndAngle=1.5708
  constraints (23):
    c: Coincident(g0,g1)
    c: Horizontal(g0)
    c: Horizontal(g2)
    c: Vertical(g1)
    c: DistanceX(g0,g0) = 56.5
    c: Horizontal(g7)
    c: Radius(g3) = 15
    c: Tangent(g7,g5) = 1.5708
    c: Tangent(g4,g3) = 1.5708
    c: Tangent(g3,g2) = -1.5708
    c: Tangent(g7,g4) = 1.5708
    c: Tangent(g6,g5) = 1.5708
    c: Tangent(g6,g0) = -1.5708
    c: Equal(g3,g6)
    c: Equal(g4,g5)
    c: DistanceY(g0,g5) = 12.5
    c: DistanceX(g2,g0) = 80
    c: DistanceX(g4,g5) = 20
    c: Tangent(g3,g-1)
    c: Tangent(g2,g8) = -1.5708
    c: Tangent(g1,g8) = -1.5708
    c: Radius(g8) = 5
    c: Coincident(g0,g-1)
FEATURE [Sketcher::SketchObject] Sketch1348
  MapMode = 5
  Support = -> [XY_Plane475]
  sketch-geometry (4):
    g0: LineSegment StartX=-10 StartY=20.15 StartZ=0 EndX=10 EndY=20.15 EndZ=0
    g1: LineSegment StartX=10 StartY=20.15 StartZ=0 EndX=10 EndY=-20.15 EndZ=0
    g2: LineSegment StartX=10 StartY=-20.15 StartZ=0 EndX=-10 EndY=-20.15 EndZ=0
    g3: LineSegment StartX=-10 StartY=-20.15 StartZ=0 EndX=-10 EndY=20.15 EndZ=0
  constraints (10):
    c: Coincident(g0,g1)
    c: Coincident(g1,g2)
    c: Coincident(g2,g3)
    c: Coincident(g3,g0)
    c: Horizontal(g2)
    c: Vertical(g3)
    c: DistanceX(g0,g0) = 20
    c: DistanceY(g1,g1) = 40.3
    c: Symmetric(g0,g1,g-1)
    c: Symmetric(g0,g0,g-2)
FEATURE [Sketcher::SketchObject] Sketch1349
  MapMode = 5
  Placement = pos=(0,0,0) rot=(1,0,0;1.5708rad)
  Support = -> [XZ_Plane487]
  sketch-geometry (2):
    g0: ArcOfCircle CenterX=0 CenterY=0 CenterZ=0 NormalX=0 NormalY=0 NormalZ=1 AngleXU=0 Radius=20 StartAngle=-1.8e-15 EndAngle=3.14159
    g1: LineSegment StartX=-20 StartY=-1.38798e-11 StartZ=0 EndX=20 EndY=-3.55e-14 EndZ=0
  constraints (6):
    c: Coincident(g0,g-1)
    c: PointOnObject(g0,g-1)
    c: PointOnObject(g0,g-1)
    c: Coincident(g1,g0)
    c: Coincident(g1,g0)
    c: Radius(g0) = 20
FEATURE [Sketcher::SketchObject] Sketch1352
  MapMode = 5
  Support = -> [XY_Plane474]
  sketch-geometry (3):
    g0: Circle [constr] CenterX=0 CenterY=0 CenterZ=0 NormalX=0 NormalY=0 NormalZ=1 AngleXU=0 Radius=20
    g1: Circle CenterX=18.1039 CenterY=8.5 CenterZ=0 NormalX=0 NormalY=0 NormalZ=1 AngleXU=0 Radius=1.25
    g2: Circle CenterX=18.1039 CenterY=-8.5 CenterZ=0 NormalX=0 NormalY=0 NormalZ=1 AngleXU=0 Radius=1.25
  constraints (7):
    c: Coincident(g0,g-1)
    c: Radius(g0) = 20
    c: PointOnObject(g1,g0)
    c: Radius(g1) = 1.25
    c: DistanceY(g-1,g1) = 8.5
    c: Equal(g2,g1)
    c: Symmetric(g2,g1,g-1)
FEATURE [Sketcher::SketchObject] Sketch1353
  MapMode = 5
  Placement = pos=(0,0,0) rot=(1,0,0;1.5708rad)
  Support = -> [XZ_Plane487]
  sketch-geometry (6):
    g0: LineSegment StartX=-15 StartY=0 StartZ=0 EndX=-25 EndY=7.5 EndZ=0
    g1: LineSegment StartX=-25 StartY=7.5 StartZ=0 EndX=-25 EndY=-7.5 EndZ=0
    g2: LineSegment StartX=-25 StartY=-7.5 StartZ=0 EndX=25 EndY=-7.5 EndZ=0
    g3: LineSegment StartX=25 StartY=-7.5 StartZ=0 EndX=25 EndY=7.5 EndZ=0
    g4: LineSegment StartX=25 StartY=7.5 StartZ=0 EndX=15 EndY=0 EndZ=0
    g5: LineSegment StartX=15 StartY=0 StartZ=0 EndX=-15 EndY=0 EndZ=0
  constraints (15):
    c: PointOnObject(g0,g-1)
    c: Coincident(g0,g1)
    c: Vertical(g1)
    c: Coincident(g1,g2)
    c: Horizontal(g2)
    c: Coincident(g2,g3)
    c: Coincident(g3,g4)
    c: Coincident(g4,g5)
    c: Coincident(g5,g0)
    c: DistanceX(g5,g5) = 30
    c: DistanceX(g4,g2) = 10
    c: Symmetric(g0,g4,g-2)
    c: Symmetric(g0,g3,g-2)
    c: DistanceY(g-1,g3) = 7.5
    c: Symmetric(g2,g3,g-1)
FEATURE [Sketcher::SketchObject] Sketch1354
  MapMode = 5
  Placement = pos=(0,0,0) rot=(1,0,0;1.5708rad)
  Support = -> [XZ_Plane487]
  sketch-geometry (8):
    g0: LineSegment [constr] StartX=-4e-16 StartY=6.69726 StartZ=0 EndX=-2.9 EndY=5.02295 EndZ=0
    g1: LineSegment [constr] StartX=-2.9 StartY=5.02295 StartZ=0 EndX=-2.9 EndY=1.67432 EndZ=0
    g2: LineSegment [constr] StartX=-2.9 StartY=1.67432 StartZ=0 EndX=0 EndY=0 EndZ=0
    g3: LineSegment [constr] StartX=0 StartY=0 StartZ=0 EndX=2.9 EndY=1.67432 EndZ=0
    g4: LineSegment [constr] StartX=2.9 StartY=1.67432 StartZ=0 EndX=2.9 EndY=5.02295 EndZ=0
    g5: LineSegment [constr] StartX=2.9 StartY=5.02295 StartZ=0 EndX=-4e-16 EndY=6.69726 EndZ=0
    g6: Circle [constr] CenterX=0 CenterY=3.34863 CenterZ=0 NormalX=0 NormalY=0 NormalZ=1 AngleXU=0 Radius=3.34863
    g7: Circle CenterX=0 CenterY=3.34863 CenterZ=0 NormalX=0 NormalY=0 NormalZ=1 AngleXU=0 Radius=1.6
  constraints (18):
    c: Coincident(g0,g1)
    c: Coincident(g1,g2)
    c: Coincident(g2,g3)
    c: Coincident(g3,g4)
    c: Coincident(g4,g5)
    c: Coincident(g5,g0)
    c: Equal(g0, g1-g5) x5
    c: PointOnObject(g0,g6)
    c: PointOnObject(g1,g6)
    c: PointOnObject(g2,g6)
    c: PointOnObject(g3,g6)
    c: PointOnObject(g4,g6)
    c: PointOnObject(g5,g6)
    c: PointOnObject(g6,g-2)
    c: DistanceX(g0,g4) = 5.8
    c: Coincident(g2,g-1)
    c: Coincident(g7,g6)
    c: Radius(g7) = 1.6
FEATURE [Sketcher::SketchObject] Sketch1358
  MapMode = 5
  Placement = pos=(0,0,0) rot=(1,0,0;1.5708rad)
  Support = -> [XZ_Plane487]
  sketch-geometry (2):
    g0: ArcOfCircle CenterX=0 CenterY=0 CenterZ=0 NormalX=0 NormalY=0 NormalZ=1 AngleXU=0 Radius=12.75 StartAngle=0 EndAngle=3.14159
    g1: LineSegment StartX=-12.75 StartY=0 StartZ=0 EndX=12.75 EndY=0 EndZ=0
  constraints (6):
    c: Coincident(g0,g-1)
    c: Coincident(g1,g0)
    c: Coincident(g1,g0)
    c: Horizontal(g1)
    c: PointOnObject(g0,g1)
    c: Radius(g0) = 12.75
FEATURE [Sketcher::SketchObject] Sketch1359
  MapMode = 5
  Support = -> [XY_Plane470]
  sketch-geometry (8):
    g0: LineSegment StartX=0 StartY=3.17543 StartZ=0 EndX=-2.75 EndY=1.58771 EndZ=0
    g1: LineSegment StartX=-2.75 StartY=1.58771 StartZ=0 EndX=-2.75 EndY=-1.58771 EndZ=0
    g2: LineSegment StartX=-2.75 StartY=-1.58771 StartZ=0 EndX=0 EndY=-3.17543 EndZ=0
    g3: LineSegment StartX=0 StartY=-3.17543 StartZ=0 EndX=2.75 EndY=-1.58771 EndZ=0
    g4: LineSegment StartX=2.75 StartY=-1.58771 StartZ=0 EndX=2.75 EndY=1.58771 EndZ=0
    g5: LineSegment StartX=2.75 StartY=1.58771 StartZ=0 EndX=0 EndY=3.17543 EndZ=0
    g6: Circle [constr] CenterX=0 CenterY=0 CenterZ=0 NormalX=0 NormalY=0 NormalZ=1 AngleXU=0 Radius=3.17543
    g7: Circle CenterX=0 CenterY=0 CenterZ=0 NormalX=0 NormalY=0 NormalZ=1 AngleXU=0 Radius=1.5
  constraints (18):
    c: Coincident(g0,g1)
    c: Coincident(g1,g2)
    c: Coincident(g2,g3)
    c: Coincident(g3,g4)
    c: Coincident(g4,g5)
    c: Coincident(g5,g0)
    c: Equal(g0, g1-g5) x5
    c: PointOnObject(g0,g6)
    c: PointOnObject(g1,g6)
    c: PointOnObject(g2,g6)
    c: PointOnObject(g3,g6)
    c: PointOnObject(g4,g6)
    c: PointOnObject(g5,g6)
    c: Coincident(g6,g-1)
    c: PointOnObject(g5,g-2)
    c: DistanceX(g0,g4) = 5.5
    c: Coincident(g7,g-1)
    c: Radius(g7) = 1.5
FEATURE [Sketcher::SketchObject] Sketch1366
  MapMode = 5
  Support = -> [XY_Plane487]
  sketch-geometry (1):
    g0: Circle CenterX=0 CenterY=0 CenterZ=0 NormalX=0 NormalY=0 NormalZ=1 AngleXU=0 Radius=2.75
  constraints (2):
    c: Coincident(g0,g-1)
    c: Radius(g0) = 2.75
FEATURE [Sketcher::SketchObject] Sketch1367
  MapMode = 5
  Support = -> [XY_Plane479]
  sketch-geometry (8):
    g0: LineSegment StartX=0 StartY=3.17543 StartZ=0 EndX=-2.75 EndY=1.58771 EndZ=0
    g1: LineSegment StartX=-2.75 StartY=1.58771 StartZ=0 EndX=-2.75 EndY=-1.58771 EndZ=0
    g2: LineSegment StartX=-2.75 StartY=-1.58771 StartZ=0 EndX=0 EndY=-3.17543 EndZ=0
    g3: LineSegment StartX=0 StartY=-3.17543 StartZ=0 EndX=2.75 EndY=-1.58771 EndZ=0
    g4: LineSegment StartX=2.75 StartY=-1.58771 StartZ=0 EndX=2.75 EndY=1.58771 EndZ=0
    g5: LineSegment StartX=2.75 StartY=1.58771 StartZ=0 EndX=0 EndY=3.17543 EndZ=0
    g6: Circle [constr] CenterX=0 CenterY=0 CenterZ=0 NormalX=0 NormalY=0 NormalZ=1 AngleXU=0 Radius=3.17543
    g7: Circle CenterX=0 CenterY=0 CenterZ=0 NormalX=0 NormalY=0 NormalZ=1 AngleXU=0 Radius=1.5
  constraints (18):
    c: Coincident(g0,g1)
    c: Coincident(g1,g2)
    c: Coincident(g2,g3)
    c: Coincident(g3,g4)
    c: Coincident(g4,g5)
    c: Coincident(g5,g0)
    c: Equal(g0, g1-g5) x5
    c: PointOnObject(g0,g6)
    c: PointOnObject(g1,g6)
    c: PointOnObject(g2,g6)
    c: PointOnObject(g3,g6)
    c: PointOnObject(g4,g6)
    c: PointOnObject(g5,g6)
    c: Coincident(g6,g-1)
    c: PointOnObject(g5,g-2)
    c: DistanceX(g0,g4) = 5.5
    c: Coincident(g7,g-1)
    c: Radius(g7) = 1.5
FEATURE [Sketcher::SketchObject] Sketch1368
  MapMode = 5
  Support = -> [XY_Plane483]
  sketch-geometry (1):
    g0: Circle CenterX=0 CenterY=0 CenterZ=0 NormalX=0 NormalY=0 NormalZ=1 AngleXU=0 Radius=1.9
  constraints (2):
    c: Coincident(g0,g-1)
    c: Radius(g0) = 1.9
FEATURE [PartDesign::Pad] Pad491  label="M3x8 Head057"
  Length = 2
  Length2 = 100
  Profile = -> Sketch1146
  Type = 0
FEATURE [Sketcher::SketchObject] Sketch1144
  MapMode = 5
  Placement = pos=(0,0,2) rot=(0,0,1;0rad)
  Support = -> [Pad491]
  sketch-geometry (1):
    g0: Circle CenterX=0 CenterY=0 CenterZ=0 NormalX=0 NormalY=0 NormalZ=1 AngleXU=0 Radius=1
  constraints (2):
    c: Coincident(g0,g-1)
    c: Radius(g0) = 1
FEATURE [PartDesign::Pad] Pad494  label="M3 Nut Primitive094"
  Length = 0.6
  Length2 = 0.6
  Profile = -> Sketch1151
  Type = 4
FEATURE [Sketcher::SketchObject] Sketch1135
  ExternalGeometry = -> [Pad494]
  MapMode = 5
  Placement = pos=(0,0,0) rot=(0.57735,0.57735,0.57735;2.0944rad)
  Support = -> [YZ_Plane541]
  sketch-geometry (6):
    g0: LineSegment StartX=-1.9594 StartY=0.6 StartZ=0 EndX=-2.8094 EndY=0.6 EndZ=0
    g1: LineSegment StartX=-2.8094 StartY=0.6 StartZ=0 EndX=-2.8094 EndY=-0.6 EndZ=0
    g2: LineSegment StartX=-2.8094 StartY=-0.6 StartZ=0 EndX=-1.9594 EndY=-0.6 EndZ=0
    g3: LineSegment StartX=-1.9594 StartY=-0.6 StartZ=0 EndX=-2.3094 EndY=-0.4 EndZ=0
    g4: LineSegment StartX=-2.3094 StartY=-0.4 StartZ=0 EndX=-2.3094 EndY=0.4 EndZ=0
    g5: LineSegment StartX=-2.3094 StartY=0.4 StartZ=0 EndX=-1.9594 EndY=0.6 EndZ=0
  constraints (15):
    c: Horizontal(g0)
    c: Coincident(g0,g1)
    c: Coincident(g1,g2)
    c: Coincident(g2,g3)
    c: Coincident(g3,g4)
    c: Coincident(g4,g5)
    c: Coincident(g5,g0)
    c: Symmetric(g4,g3,g-1)
    c: Symmetric(g0,g2,g-1)
    c: Symmetric(g1,g0,g-1)
    c: DistanceX(g0,g4) = 0.5
    c: DistanceY(g3,g4) = 0.8
    c: DistanceY(g1,g0) = 1.2
    c: PointOnObject(g3,g-3)
    c: DistanceX(g4,g0) = 0.35
FEATURE [PartDesign::Pocket] Pocket449  label="Ball Bearing Mount Pocket005"
  BaseFeature = -> Pocket433
  Length = 5
  Length2 = 100
  Profile = -> Pocket433 [Face3]
  Type = 0
FEATURE [PartDesign::Pad] Pad501  label="M3x8 Head058"
  Length = 2
  Length2 = 100
  Profile = -> Sketch1159
  Type = 0
FEATURE [Sketcher::SketchObject] Sketch1143
  MapMode = 5
  Placement = pos=(0,0,2) rot=(0,0,1;0rad)
  Support = -> [Pad501]
  sketch-geometry (1):
    g0: Circle CenterX=0 CenterY=0 CenterZ=0 NormalX=0 NormalY=0 NormalZ=1 AngleXU=0 Radius=1
  constraints (2):
    c: Coincident(g0,g-1)
    c: Radius(g0) = 1
FEATURE [PartDesign::Pad] Pad502  label="M3x8 Thread057"
  BaseFeature = -> Pad491
  Length = 8
  Length2 = 100
  Profile = -> Sketch1144
  Type = 0
FEATURE [Sketcher::SketchObject] Sketch1150
  MapMode = 5
  Placement = pos=(0,0,0) rot=(1,0,0;3.14159rad)
  Support = -> [Pad502]
  sketch-geometry (7):
    g0: LineSegment StartX=0.77 StartY=0.44456 StartZ=0 EndX=0 EndY=0.889119 EndZ=0
    g1: LineSegment StartX=0 StartY=0.889119 StartZ=0 EndX=-0.77 EndY=0.44456 EndZ=0
    g2: LineSegment StartX=-0.77 StartY=0.44456 StartZ=0 EndX=-0.77 EndY=-0.44456 EndZ=0
    g3: LineSegment StartX=-0.77 StartY=-0.44456 StartZ=0 EndX=3.85628e-11 EndY=-0.889119 EndZ=0
    g4: LineSegment StartX=3.85628e-11 StartY=-0.889119 StartZ=0 EndX=0.77 EndY=-0.44456 EndZ=0
    g5: LineSegment StartX=0.77 StartY=-0.44456 StartZ=0 EndX=0.77 EndY=0.44456 EndZ=0
    g6: Circle [constr] CenterX=0 CenterY=0 CenterZ=0 NormalX=0 NormalY=0 NormalZ=1 AngleXU=0 Radius=0.889119
  constraints (16):
    c: Coincident(g0,g1)
    c: Coincident(g1,g2)
    c: Coincident(g2,g3)
    c: Coincident(g3,g4)
    c: Coincident(g4,g5)
    c: Coincident(g5,g0)
    c: Equal(g0, g1-g5) x5
    c: PointOnObject(g0,g6)
    c: PointOnObject(g1,g6)
    c: PointOnObject(g2,g6)
    c: PointOnObject(g3,g6)
    c: PointOnObject(g4,g6)
    c: PointOnObject(g5,g6)
    c: Coincident(g6,g-1)
    c: PointOnObject(g0,g-2)
    c: DistanceX(g1,g0) = 1.54
FEATURE [PartDesign::Pad] Pad503
  Length = 2
  Length2 = 100
  Profile = -> Sketch1117
  Type = 0
FEATURE [Sketcher::SketchObject] Sketch1119
  MapMode = 5
  Placement = pos=(0,0,2) rot=(0,0,1;0rad)
  Support = -> [Pad503]
  sketch-geometry (2):
    g0: Circle CenterX=0 CenterY=0 CenterZ=0 NormalX=0 NormalY=0 NormalZ=1 AngleXU=0 Radius=5
    g1: Circle CenterX=0 CenterY=0 CenterZ=0 NormalX=0 NormalY=0 NormalZ=1 AngleXU=0 Radius=3.5
  constraints (4):
    c: Coincident(g0,g-1)
    c: Coincident(g1,g0)
    c: Radius(g1) = 3.5
    c: Radius(g0) = 5
FEATURE [PartDesign::Pocket] Pocket455
  BaseFeature = -> Pad503
  Length = 1
  Length2 = 100
  Profile = -> Sketch1119
  Type = 0
FEATURE [Sketcher::SketchObject] Sketch1122
  MapMode = 5
  Placement = pos=(0,0,2) rot=(0,0,1;0rad)
  Support = -> [Pocket455]
  sketch-geometry (1):
    g0: Circle CenterX=0 CenterY=0 CenterZ=0 NormalX=0 NormalY=0 NormalZ=1 AngleXU=0 Radius=3
  constraints (2):
    c: Coincident(g0,g-1)
    c: Radius(g0) = 3
FEATURE [PartDesign::Pocket] Pocket460
  BaseFeature = -> Pocket455
  Length = 1
  Length2 = 100
  Profile = -> Sketch1122
  Type = 0
FEATURE [Sketcher::SketchObject] Sketch1128
  MapMode = 5
  Placement = pos=(0,0,1) rot=(0,0,1;0rad)
  Support = -> [Pocket460]
  sketch-geometry (1):
    g0: Circle CenterX=0 CenterY=0 CenterZ=0 NormalX=0 NormalY=0 NormalZ=1 AngleXU=0 Radius=1.5
  constraints (2):
    c: Coincident(g0,g-1)
    c: Radius(g0) = 1.5
FEATURE [PartDesign::Pocket] Pocket452
  BaseFeature = -> Pocket460
  Length = 5
  Length2 = 100
  Profile = -> Sketch1128
  Type = 0
FEATURE [Sketcher::SketchObject] Sketch1127
  MapMode = 5
  Placement = pos=(0,0,0) rot=(1,0,0;3.14159rad)
  Support = -> [Pocket452]
  sketch-geometry (2):
    g0: Circle CenterX=0 CenterY=0 CenterZ=0 NormalX=0 NormalY=0 NormalZ=1 AngleXU=0 Radius=4.5
    g1: Circle CenterX=0 CenterY=0 CenterZ=0 NormalX=0 NormalY=0 NormalZ=1 AngleXU=0 Radius=3
  constraints (4):
    c: Coincident(g0,g-1)
    c: Coincident(g1,g0)
    c: Radius(g0) = 4.5
    c: Radius(g1) = 3
FEATURE [PartDesign::Pad] Pad504  label="Baseplate023"
  Length = 5
  Length2 = 100
  Profile = -> Sketch1130
  Type = 0
FEATURE [Sketcher::SketchObject] Sketch1115
  MapMode = 5
  Placement = pos=(40,-9.6e-15,0) rot=(0.57735,0.57735,0.57735;2.0944rad)
  Support = -> [Pad504]
  sketch-geometry (4):
    g0: ArcOfCircle CenterX=35 CenterY=-21 CenterZ=0 NormalX=0 NormalY=0 NormalZ=1 AngleXU=0 Radius=26 StartAngle=1.17601 EndAngle=1.5708
    g1: LineSegment StartX=35 StartY=5 StartZ=0 EndX=35 EndY=6 EndZ=0
    g2: LineSegment StartX=35 StartY=6 StartZ=0 EndX=45 EndY=6 EndZ=0
    g3: LineSegment StartX=45 StartY=6 StartZ=0 EndX=45 EndY=3 EndZ=0
  constraints (13):
    c: Coincident(g1,g0)
    c: Vertical(g1)
    c: Horizontal(g2)
    c: Coincident(g3,g2)
    c: Vertical(g3)
    c: Coincident(g0,g3)
    c: Coincident(g1,g2)
    c: DistanceY(g1,g1) = 1
    c: DistanceY(g3,g3) = 3
    c: DistanceX(g2,g2) = 10
    c: DistanceY(g-1,g0) = 5
    c: DistanceX(g-1,g0) = 45
    c: Perpendicular(g0,g1)
FEATURE [PartDesign::SubtractivePipe] SubtractivePipe011  label="Smooth Surfaces005"
  AuxilleryCurvelinear = true
  AuxillerySpineTangent = false
  BaseFeature = -> Pad504
  Binormal = (0,0,0)
  Mode = 0
  Profile = -> Sketch1115
  Spine = -> Pad504 [Edge19,Edge22,Edge24,Edge4,Edge7,Edge10,Edge13]
  SpineTangent = false
  Transformation = 0
  Transition = 0
FEATURE [Sketcher::SketchObject] Sketch1134
  MapMode = 5
  Placement = pos=(0,0,5) rot=(0,0,1;0rad)
  Support = -> [SubtractivePipe011]
  sketch-geometry (3):
    g0: Circle [constr] CenterX=0 CenterY=15 CenterZ=0 NormalX=0 NormalY=0 NormalZ=1 AngleXU=0 Radius=35
    g1: Circle CenterX=28.7228 CenterY=35 CenterZ=0 NormalX=0 NormalY=0 NormalZ=1 AngleXU=0 Radius=2.85
    g2: Circle CenterX=33.541 CenterY=25 CenterZ=0 NormalX=0 NormalY=0 NormalZ=1 AngleXU=0 Radius=2.85
  constraints (9):
    c: PointOnObject(g1,g0)
    c: PointOnObject(g2,g0)
    c: Radius(g0) = 35
    c: Equal(g2,g1)
    c: Radius(g1) = 2.85
    c: DistanceY(g2,g1) = 10
    c: DistanceY(g-1,g0) = 15
    c: DistanceY(g0,g2) = 10
    c: DistanceX(g-1,g0) = 0
FEATURE [PartDesign::Pad] Pad505  label="M3 Nut Primitive098"
  Length = 0.6
  Length2 = 0.6
  Profile = -> Sketch1156
  Type = 4
FEATURE [Sketcher::SketchObject] Sketch1138
  ExternalGeometry = -> [Pad505]
  MapMode = 5
  Placement = pos=(0,0,0) rot=(0.57735,0.57735,0.57735;2.0944rad)
  Support = -> [YZ_Plane572]
  sketch-geometry (6):
    g0: LineSegment StartX=-1.9594 StartY=0.6 StartZ=0 EndX=-2.8094 EndY=0.6 EndZ=0
    g1: LineSegment StartX=-2.8094 StartY=0.6 StartZ=0 EndX=-2.8094 EndY=-0.6 EndZ=0
    g2: LineSegment StartX=-2.8094 StartY=-0.6 StartZ=0 EndX=-1.9594 EndY=-0.6 EndZ=0
    g3: LineSegment StartX=-1.9594 StartY=-0.6 StartZ=0 EndX=-2.3094 EndY=-0.4 EndZ=0
    g4: LineSegment StartX=-2.3094 StartY=-0.4 StartZ=0 EndX=-2.3094 EndY=0.4 EndZ=0
    g5: LineSegment StartX=-2.3094 StartY=0.4 StartZ=0 EndX=-1.9594 EndY=0.6 EndZ=0
  constraints (15):
    c: Horizontal(g0)
    c: Coincident(g0,g1)
    c: Coincident(g1,g2)
    c: Coincident(g2,g3)
    c: Coincident(g3,g4)
    c: Coincident(g4,g5)
    c: Coincident(g5,g0)
    c: Symmetric(g4,g3,g-1)
    c: Symmetric(g0,g2,g-1)
    c: Symmetric(g1,g0,g-1)
    c: DistanceX(g0,g4) = 0.5
    c: DistanceY(g3,g4) = 0.8
    c: DistanceY(g1,g0) = 1.2
    c: PointOnObject(g3,g-3)
    c: DistanceX(g4,g0) = 0.35
FEATURE [PartDesign::Groove] Groove101  label="M3 Nut Smooth097"
  Angle = 360
  Axis = (-2e-16,3e-16,1)
  Base = (0,0,0)
  BaseFeature = -> Pad505
  Profile = -> Sketch1138
  ReferenceAxis = -> Sketch1138 [V_Axis]
  Reversed = true
FEATURE [PartDesign::Pad] Pad508  label="M3 Nut Primitive099"
  Length = 0.6
  Length2 = 0.6
  Profile = -> Sketch1148
  Type = 4
FEATURE [Sketcher::SketchObject] Sketch1168
  ExternalGeometry = -> [Pad508]
  MapMode = 5
  Placement = pos=(0,0,0) rot=(0.57735,0.57735,0.57735;2.0944rad)
  Support = -> [YZ_Plane553]
  sketch-geometry (6):
    g0: LineSegment StartX=-1.9594 StartY=0.6 StartZ=0 EndX=-2.8094 EndY=0.6 EndZ=0
    g1: LineSegment StartX=-2.8094 StartY=0.6 StartZ=0 EndX=-2.8094 EndY=-0.6 EndZ=0
    g2: LineSegment StartX=-2.8094 StartY=-0.6 StartZ=0 EndX=-1.9594 EndY=-0.6 EndZ=0
    g3: LineSegment StartX=-1.9594 StartY=-0.6 StartZ=0 EndX=-2.3094 EndY=-0.4 EndZ=0
    g4: LineSegment StartX=-2.3094 StartY=-0.4 StartZ=0 EndX=-2.3094 EndY=0.4 EndZ=0
    g5: LineSegment StartX=-2.3094 StartY=0.4 StartZ=0 EndX=-1.9594 EndY=0.6 EndZ=0
  constraints (15):
    c: Horizontal(g0)
    c: Coincident(g0,g1)
    c: Coincident(g1,g2)
    c: Coincident(g2,g3)
    c: Coincident(g3,g4)
    c: Coincident(g4,g5)
    c: Coincident(g5,g0)
    c: Symmetric(g4,g3,g-1)
    c: Symmetric(g0,g2,g-1)
    c: Symmetric(g1,g0,g-1)
    c: DistanceX(g0,g4) = 0.5
    c: DistanceY(g3,g4) = 0.8
    c: DistanceY(g1,g0) = 1.2
    c: PointOnObject(g3,g-3)
    c: DistanceX(g4,g0) = 0.35
FEATURE [PartDesign::Groove] Groove099  label="M3 Nut Smooth095"
  Angle = 360
  Axis = (-2e-16,3e-16,1)
  Base = (0,0,0)
  BaseFeature = -> Pad508
  Profile = -> Sketch1168
  ReferenceAxis = -> Sketch1168 [V_Axis]
  Reversed = true
FEATURE [PartDesign::Pocket] Pocket469  label="M3x8 Wrench059"
  BaseFeature = -> Pad502
  Length = 1
  Length2 = 100
  Profile = -> Sketch1150
  Type = 0
FEATURE [PartDesign::Groove] Groove103  label="M3 Nut Smooth099"
  Angle = 360
  Axis = (-2e-16,3e-16,1)
  Base = (0,0,0)
  BaseFeature = -> Pad494
  Profile = -> Sketch1135
  ReferenceAxis = -> Sketch1135 [V_Axis]
  Reversed = true
FEATURE [PartDesign::Pad] Pad510  label="Baseplate024"
  Length = 5
  Length2 = 100
  Profile = -> Sketch1306
  Type = 0
FEATURE [Sketcher::SketchObject] Sketch1312
  MapMode = 5
  Placement = pos=(-40,0,0) rot=(0.57735,-0.57735,-0.57735;2.0944rad)
  Support = -> [Pad510]
  sketch-geometry (4):
    g0: ArcOfCircle CenterX=-25 CenterY=-21 CenterZ=0 NormalX=0 NormalY=0 NormalZ=1 AngleXU=0 Radius=26 StartAngle=1.17601 EndAngle=1.5708
    g1: LineSegment StartX=-25 StartY=5 StartZ=0 EndX=-25 EndY=6 EndZ=0
    g2: LineSegment StartX=-25 StartY=6 StartZ=0 EndX=-15 EndY=6 EndZ=0
    g3: LineSegment StartX=-15 StartY=6 StartZ=0 EndX=-15 EndY=3 EndZ=0
  constraints (13):
    c: Coincident(g1,g0)
    c: Vertical(g1)
    c: Horizontal(g2)
    c: Coincident(g3,g2)
    c: Vertical(g3)
    c: Coincident(g0,g3)
    c: Coincident(g1,g2)
    c: DistanceY(g1,g1) = 1
    c: DistanceY(g3,g3) = 3
    c: DistanceX(g2,g2) = 10
    c: DistanceY(g-1,g0) = 5
    c: Perpendicular(g0,g1)
    c: DistanceX(g0,g-1) = 15
FEATURE [PartDesign::SubtractivePipe] SubtractivePipe015  label="Smooth Surfaces006"
  AuxilleryCurvelinear = true
  AuxillerySpineTangent = false
  BaseFeature = -> Pad510
  Binormal = (0,0,0)
  Mode = 0
  Profile = -> Sketch1312
  Spine = -> Pad510 [Edge19,Edge22,Edge24,Edge4,Edge7,Edge10,Edge13]
  SpineTangent = false
  Transformation = 0
  Transition = 0
FEATURE [Sketcher::SketchObject] Sketch1172
  MapMode = 5
  Placement = pos=(0,0,5) rot=(0,0,1;0rad)
  Support = -> [SubtractivePipe015]
  sketch-geometry (3):
    g0: Circle [constr] CenterX=0 CenterY=15 CenterZ=0 NormalX=0 NormalY=0 NormalZ=1 AngleXU=0 Radius=35
    g1: Circle CenterX=-33.541 CenterY=25 CenterZ=0 NormalX=0 NormalY=0 NormalZ=1 AngleXU=0 Radius=2.85
    g2: Circle CenterX=-28.7228 CenterY=35 CenterZ=0 NormalX=0 NormalY=0 NormalZ=1 AngleXU=0 Radius=2.85
  constraints (9):
    c: PointOnObject(g1,g0)
    c: PointOnObject(g2,g0)
    c: Radius(g0) = 35
    c: Equal(g2,g1)
    c: Radius(g1) = 2.85
    c: DistanceY(g1,g2) = 10
    c: DistanceY(g-1,g0) = 15
    c: DistanceY(g0,g1) = 10
    c: DistanceX(g0,g-1) = 0
FEATURE [PartDesign::Pad] Pad511
  BaseFeature = -> Pocket452
  Length = 3
  Length2 = 100
  Profile = -> Sketch1127
  Type = 0
FEATURE [PartDesign::Pad] Pad512  label="M3x8 Thread061"
  BaseFeature = -> Pad501
  Length = 8
  Length2 = 100
  Profile = -> Sketch1143
  Type = 0
FEATURE [Sketcher::SketchObject] Sketch1147
  MapMode = 5
  Placement = pos=(0,0,0) rot=(1,0,0;3.14159rad)
  Support = -> [Pad512]
  sketch-geometry (7):
    g0: LineSegment StartX=0.77 StartY=0.44456 StartZ=0 EndX=0 EndY=0.889119 EndZ=0
    g1: LineSegment StartX=0 StartY=0.889119 StartZ=0 EndX=-0.77 EndY=0.44456 EndZ=0
    g2: LineSegment StartX=-0.77 StartY=0.44456 StartZ=0 EndX=-0.77 EndY=-0.44456 EndZ=0
    g3: LineSegment StartX=-0.77 StartY=-0.44456 StartZ=0 EndX=3.85628e-11 EndY=-0.889119 EndZ=0
    g4: LineSegment StartX=3.85628e-11 StartY=-0.889119 StartZ=0 EndX=0.77 EndY=-0.44456 EndZ=0
    g5: LineSegment StartX=0.77 StartY=-0.44456 StartZ=0 EndX=0.77 EndY=0.44456 EndZ=0
    g6: Circle [constr] CenterX=0 CenterY=0 CenterZ=0 NormalX=0 NormalY=0 NormalZ=1 AngleXU=0 Radius=0.889119
  constraints (16):
    c: Coincident(g0,g1)
    c: Coincident(g1,g2)
    c: Coincident(g2,g3)
    c: Coincident(g3,g4)
    c: Coincident(g4,g5)
    c: Coincident(g5,g0)
    c: Equal(g0, g1-g5) x5
    c: PointOnObject(g0,g6)
    c: PointOnObject(g1,g6)
    c: PointOnObject(g2,g6)
    c: PointOnObject(g3,g6)
    c: PointOnObject(g4,g6)
    c: PointOnObject(g5,g6)
    c: Coincident(g6,g-1)
    c: PointOnObject(g0,g-2)
    c: DistanceX(g1,g0) = 1.54
FEATURE [PartDesign::Pocket] Pocket467  label="M3x8 Wrench058"
  BaseFeature = -> Pad512
  Length = 1
  Length2 = 100
  Profile = -> Sketch1147
  Type = 0
FEATURE [PartDesign::Pad] Pad513  label="M3x8 Head059"
  Length = 2
  Length2 = 100
  Profile = -> Sketch1149
  Type = 0
FEATURE [Sketcher::SketchObject] Sketch1157
  MapMode = 5
  Placement = pos=(0,0,2) rot=(0,0,1;0rad)
  Support = -> [Pad513]
  sketch-geometry (1):
    g0: Circle CenterX=0 CenterY=0 CenterZ=0 NormalX=0 NormalY=0 NormalZ=1 AngleXU=0 Radius=1
  constraints (2):
    c: Coincident(g0,g-1)
    c: Radius(g0) = 1
FEATURE [PartDesign::Pad] Pad507  label="M3x8 Thread059"
  BaseFeature = -> Pad513
  Length = 8
  Length2 = 100
  Profile = -> Sketch1157
  Type = 0
FEATURE [Sketcher::SketchObject] Sketch1153
  MapMode = 5
  Placement = pos=(0,0,0) rot=(1,0,0;3.14159rad)
  Support = -> [Pad507]
  sketch-geometry (7):
    g0: LineSegment StartX=0.77 StartY=0.44456 StartZ=0 EndX=0 EndY=0.889119 EndZ=0
    g1: LineSegment StartX=0 StartY=0.889119 StartZ=0 EndX=-0.77 EndY=0.44456 EndZ=0
    g2: LineSegment StartX=-0.77 StartY=0.44456 StartZ=0 EndX=-0.77 EndY=-0.44456 EndZ=0
    g3: LineSegment StartX=-0.77 StartY=-0.44456 StartZ=0 EndX=3.85628e-11 EndY=-0.889119 EndZ=0
    g4: LineSegment StartX=3.85628e-11 StartY=-0.889119 StartZ=0 EndX=0.77 EndY=-0.44456 EndZ=0
    g5: LineSegment StartX=0.77 StartY=-0.44456 StartZ=0 EndX=0.77 EndY=0.44456 EndZ=0
    g6: Circle [constr] CenterX=0 CenterY=0 CenterZ=0 NormalX=0 NormalY=0 NormalZ=1 AngleXU=0 Radius=0.889119
  constraints (16):
    c: Coincident(g0,g1)
    c: Coincident(g1,g2)
    c: Coincident(g2,g3)
    c: Coincident(g3,g4)
    c: Coincident(g4,g5)
    c: Coincident(g5,g0)
    c: Equal(g0, g1-g5) x5
    c: PointOnObject(g0,g6)
    c: PointOnObject(g1,g6)
    c: PointOnObject(g2,g6)
    c: PointOnObject(g3,g6)
    c: PointOnObject(g4,g6)
    c: PointOnObject(g5,g6)
    c: Coincident(g6,g-1)
    c: PointOnObject(g0,g-2)
    c: DistanceX(g1,g0) = 1.54
FEATURE [PartDesign::Pad] Pad514  label="M3 Nut Primitive100"
  Length = 0.6
  Length2 = 0.6
  Profile = -> Sketch1131
  Type = 4
FEATURE [Sketcher::SketchObject] Sketch1120
  ExternalGeometry = -> [Pad514]
  MapMode = 5
  Placement = pos=(0,0,0) rot=(0.57735,0.57735,0.57735;2.0944rad)
  Support = -> [YZ_Plane552]
  sketch-geometry (6):
    g0: LineSegment StartX=-1.9594 StartY=0.6 StartZ=0 EndX=-2.8094 EndY=0.6 EndZ=0
    g1: LineSegment StartX=-2.8094 StartY=0.6 StartZ=0 EndX=-2.8094 EndY=-0.6 EndZ=0
    g2: LineSegment StartX=-2.8094 StartY=-0.6 StartZ=0 EndX=-1.9594 EndY=-0.6 EndZ=0
    g3: LineSegment StartX=-1.9594 StartY=-0.6 StartZ=0 EndX=-2.3094 EndY=-0.4 EndZ=0
    g4: LineSegment StartX=-2.3094 StartY=-0.4 StartZ=0 EndX=-2.3094 EndY=0.4 EndZ=0
    g5: LineSegment StartX=-2.3094 StartY=0.4 StartZ=0 EndX=-1.9594 EndY=0.6 EndZ=0
  constraints (15):
    c: Horizontal(g0)
    c: Coincident(g0,g1)
    c: Coincident(g1,g2)
    c: Coincident(g2,g3)
    c: Coincident(g3,g4)
    c: Coincident(g4,g5)
    c: Coincident(g5,g0)
    c: Symmetric(g4,g3,g-1)
    c: Symmetric(g0,g2,g-1)
    c: Symmetric(g1,g0,g-1)
    c: DistanceX(g0,g4) = 0.5
    c: DistanceY(g3,g4) = 0.8
    c: DistanceY(g1,g0) = 1.2
    c: PointOnObject(g3,g-3)
    c: DistanceX(g4,g0) = 0.35
FEATURE [PartDesign::Groove] Groove102  label="M3 Nut Smooth098"
  Angle = 360
  Axis = (-2e-16,3e-16,1)
  Base = (0,0,0)
  BaseFeature = -> Pad514
  Profile = -> Sketch1120
  ReferenceAxis = -> Sketch1120 [V_Axis]
  Reversed = true
FEATURE [PartDesign::Pad] Pad515  label="M3x8 Head060"
  Length = 2
  Length2 = 100
  Profile = -> Sketch1308
  Type = 0
FEATURE [Sketcher::SketchObject] Sketch1158
  MapMode = 5
  Placement = pos=(0,0,2) rot=(0,0,1;0rad)
  Support = -> [Pad515]
  sketch-geometry (1):
    g0: Circle CenterX=0 CenterY=0 CenterZ=0 NormalX=0 NormalY=0 NormalZ=1 AngleXU=0 Radius=1
  constraints (2):
    c: Coincident(g0,g-1)
    c: Radius(g0) = 1
FEATURE [PartDesign::Pad] Pad516  label="M3x8 Head061"
  Length = 2
  Length2 = 100
  Profile = -> Sketch1368
  Type = 0
FEATURE [Sketcher::SketchObject] Sketch1272
  MapMode = 5
  Placement = pos=(0,0,2) rot=(0,0,1;0rad)
  Support = -> [Pad516]
  sketch-geometry (1):
    g0: Circle CenterX=0 CenterY=0 CenterZ=0 NormalX=0 NormalY=0 NormalZ=1 AngleXU=0 Radius=1
  constraints (2):
    c: Coincident(g0,g-1)
    c: Radius(g0) = 1
FEATURE [PartDesign::Pad] Pad517  label="M3 Nut Primitive101"
  Length = 0.6
  Length2 = 0.6
  Profile = -> Sketch1154
  Type = 4
FEATURE [Sketcher::SketchObject] Sketch1139
  ExternalGeometry = -> [Pad517]
  MapMode = 5
  Placement = pos=(0,0,0) rot=(0.57735,0.57735,0.57735;2.0944rad)
  Support = -> [YZ_Plane561]
  sketch-geometry (6):
    g0: LineSegment StartX=-1.9594 StartY=0.6 StartZ=0 EndX=-2.8094 EndY=0.6 EndZ=0
    g1: LineSegment StartX=-2.8094 StartY=0.6 StartZ=0 EndX=-2.8094 EndY=-0.6 EndZ=0
    g2: LineSegment StartX=-2.8094 StartY=-0.6 StartZ=0 EndX=-1.9594 EndY=-0.6 EndZ=0
    g3: LineSegment StartX=-1.9594 StartY=-0.6 StartZ=0 EndX=-2.3094 EndY=-0.4 EndZ=0
    g4: LineSegment StartX=-2.3094 StartY=-0.4 StartZ=0 EndX=-2.3094 EndY=0.4 EndZ=0
    g5: LineSegment StartX=-2.3094 StartY=0.4 StartZ=0 EndX=-1.9594 EndY=0.6 EndZ=0
  constraints (15):
    c: Horizontal(g0)
    c: Coincident(g0,g1)
    c: Coincident(g1,g2)
    c: Coincident(g2,g3)
    c: Coincident(g3,g4)
    c: Coincident(g4,g5)
    c: Coincident(g5,g0)
    c: Symmetric(g4,g3,g-1)
    c: Symmetric(g0,g2,g-1)
    c: Symmetric(g1,g0,g-1)
    c: DistanceX(g0,g4) = 0.5
    c: DistanceY(g3,g4) = 0.8
    c: DistanceY(g1,g0) = 1.2
    c: PointOnObject(g3,g-3)
    c: DistanceX(g4,g0) = 0.35
FEATURE [PartDesign::Groove] Groove104  label="M3 Nut Smooth100"
  Angle = 360
  Axis = (-2e-16,3e-16,1)
  Base = (0,0,0)
  BaseFeature = -> Pad517
  Profile = -> Sketch1139
  ReferenceAxis = -> Sketch1139 [V_Axis]
  Reversed = true
FEATURE [PartDesign::Pocket] Pocket475  label="M3x8 Wrench061"
  BaseFeature = -> Pad507
  Length = 1
  Length2 = 100
  Profile = -> Sketch1153
  Type = 0
FEATURE [PartDesign::Pad] Pad518  label="M3 Nut Primitive102"
  Length = 1.2
  Length2 = 1.2
  Profile = -> Sketch1359
  Type = 4
FEATURE [Sketcher::SketchObject] Sketch1364
  ExternalGeometry = -> [Pad518]
  MapMode = 5
  Placement = pos=(0,0,0) rot=(0.57735,0.57735,0.57735;2.0944rad)
  Support = -> [YZ_Plane475]
  sketch-geometry (6):
    g0: LineSegment StartX=-2.67543 StartY=1.2 StartZ=0 EndX=-3.67543 EndY=1.2 EndZ=0
    g1: LineSegment StartX=-3.67543 StartY=1.2 StartZ=0 EndX=-3.67543 EndY=-1.2 EndZ=0
    g2: LineSegment StartX=-3.67543 StartY=-1.2 StartZ=0 EndX=-2.67543 EndY=-1.2 EndZ=0
    g3: LineSegment StartX=-2.67543 StartY=-1.2 StartZ=0 EndX=-3.17543 EndY=-1 EndZ=0
    g4: LineSegment StartX=-3.17543 StartY=-1 StartZ=0 EndX=-3.17543 EndY=1 EndZ=0
    g5: LineSegment StartX=-3.17543 StartY=1 StartZ=0 EndX=-2.67543 EndY=1.2 EndZ=0
  constraints (15):
    c: Horizontal(g0)
    c: Coincident(g0,g1)
    c: Coincident(g1,g2)
    c: Coincident(g2,g3)
    c: Coincident(g3,g4)
    c: Coincident(g4,g5)
    c: Coincident(g5,g0)
    c: Symmetric(g4,g3,g-1)
    c: Symmetric(g0,g2,g-1)
    c: Symmetric(g1,g0,g-1)
    c: DistanceX(g0,g4) = 0.5
    c: DistanceY(g3,g4) = 2
    c: DistanceY(g1,g0) = 2.4
    c: PointOnObject(g3,g-3)
    c: DistanceX(g4,g0) = 0.5
FEATURE [PartDesign::Pad] Pad519  label="M3x8 Thread062"
  BaseFeature = -> Pad515
  Length = 8
  Length2 = 100
  Profile = -> Sketch1158
  Type = 0
FEATURE [Sketcher::SketchObject] Sketch1167
  MapMode = 5
  Placement = pos=(0,0,0) rot=(1,0,0;3.14159rad)
  Support = -> [Pad519]
  sketch-geometry (7):
    g0: LineSegment StartX=0.77 StartY=0.44456 StartZ=0 EndX=0 EndY=0.889119 EndZ=0
    g1: LineSegment StartX=0 StartY=0.889119 StartZ=0 EndX=-0.77 EndY=0.44456 EndZ=0
    g2: LineSegment StartX=-0.77 StartY=0.44456 StartZ=0 EndX=-0.77 EndY=-0.44456 EndZ=0
    g3: LineSegment StartX=-0.77 StartY=-0.44456 StartZ=0 EndX=3.85628e-11 EndY=-0.889119 EndZ=0
    g4: LineSegment StartX=3.85628e-11 StartY=-0.889119 StartZ=0 EndX=0.77 EndY=-0.44456 EndZ=0
    g5: LineSegment StartX=0.77 StartY=-0.44456 StartZ=0 EndX=0.77 EndY=0.44456 EndZ=0
    g6: Circle [constr] CenterX=0 CenterY=0 CenterZ=0 NormalX=0 NormalY=0 NormalZ=1 AngleXU=0 Radius=0.889119
  constraints (16):
    c: Coincident(g0,g1)
    c: Coincident(g1,g2)
    c: Coincident(g2,g3)
    c: Coincident(g3,g4)
    c: Coincident(g4,g5)
    c: Coincident(g5,g0)
    c: Equal(g0, g1-g5) x5
    c: PointOnObject(g0,g6)
    c: PointOnObject(g1,g6)
    c: PointOnObject(g2,g6)
    c: PointOnObject(g3,g6)
    c: PointOnObject(g4,g6)
    c: PointOnObject(g5,g6)
    c: Coincident(g6,g-1)
    c: PointOnObject(g0,g-2)
    c: DistanceX(g1,g0) = 1.54
FEATURE [PartDesign::Pad] Pad520  label="Baseblock011"
  Length = 15
  Length2 = 15
  Placement = pos=(0,0,0) rot=(1,0,0;1.5708rad)
  Profile = -> Sketch1349
  Type = 4
FEATURE [Sketcher::SketchObject] Sketch1338
  MapMode = 5
  Placement = pos=(0,0,-6.9576e-12) rot=(1,0,0;3.14159rad)
  Support = -> [Pad520]
  sketch-geometry (4):
    g0: ArcOfCircle CenterX=0 CenterY=0 CenterZ=0 NormalX=0 NormalY=0 NormalZ=1 AngleXU=0 Radius=20 StartAngle=2.29353 EndAngle=3.98965
    g1: LineSegment StartX=-13.2288 StartY=15 StartZ=0 EndX=-23.2288 EndY=15 EndZ=0
    g2: LineSegment StartX=-23.2288 StartY=15 StartZ=0 EndX=-23.2288 EndY=-15 EndZ=0
    g3: LineSegment StartX=-23.2288 StartY=-15 StartZ=0 EndX=-13.2288 EndY=-15 EndZ=0
  constraints (12):
    c: Coincident(g0,g-1)
    c: Vertical(g0,g0)
    c: Coincident(g0,g1)
    c: Coincident(g1,g2)
    c: Vertical(g2)
    c: Coincident(g2,g3)
    c: Coincident(g3,g0)
    c: Horizontal(g3)
    c: Radius(g0) = 20
    c: DistanceX(g1,g1) = 10
    c: DistanceY(g2,g2) = 30
    c: Horizontal(g1)
FEATURE [PartDesign::Pad] Pad521  label="M3x8 Head062"
  Length = 2
  Length2 = 100
  Profile = -> Sketch1132
  Type = 0
FEATURE [Sketcher::SketchObject] Sketch1129
  MapMode = 5
  Placement = pos=(0,0,2) rot=(0,0,1;0rad)
  Support = -> [Pad521]
  sketch-geometry (1):
    g0: Circle CenterX=0 CenterY=0 CenterZ=0 NormalX=0 NormalY=0 NormalZ=1 AngleXU=0 Radius=1
  constraints (2):
    c: Coincident(g0,g-1)
    c: Radius(g0) = 1
FEATURE [PartDesign::Pad] Pad506  label="M3x8 Thread058"
  BaseFeature = -> Pad521
  Length = 8
  Length2 = 100
  Profile = -> Sketch1129
  Type = 0
FEATURE [Sketcher::SketchObject] Sketch1140
  MapMode = 5
  Placement = pos=(0,0,0) rot=(1,0,0;3.14159rad)
  Support = -> [Pad506]
  sketch-geometry (7):
    g0: LineSegment StartX=0.77 StartY=0.44456 StartZ=0 EndX=0 EndY=0.889119 EndZ=0
    g1: LineSegment StartX=0 StartY=0.889119 StartZ=0 EndX=-0.77 EndY=0.44456 EndZ=0
    g2: LineSegment StartX=-0.77 StartY=0.44456 StartZ=0 EndX=-0.77 EndY=-0.44456 EndZ=0
    g3: LineSegment StartX=-0.77 StartY=-0.44456 StartZ=0 EndX=3.85628e-11 EndY=-0.889119 EndZ=0
    g4: LineSegment StartX=3.85628e-11 StartY=-0.889119 StartZ=0 EndX=0.77 EndY=-0.44456 EndZ=0
    g5: LineSegment StartX=0.77 StartY=-0.44456 StartZ=0 EndX=0.77 EndY=0.44456 EndZ=0
    g6: Circle [constr] CenterX=0 CenterY=0 CenterZ=0 NormalX=0 NormalY=0 NormalZ=1 AngleXU=0 Radius=0.889119
  constraints (16):
    c: Coincident(g0,g1)
    c: Coincident(g1,g2)
    c: Coincident(g2,g3)
    c: Coincident(g3,g4)
    c: Coincident(g4,g5)
    c: Coincident(g5,g0)
    c: Equal(g0, g1-g5) x5
    c: PointOnObject(g0,g6)
    c: PointOnObject(g1,g6)
    c: PointOnObject(g2,g6)
    c: PointOnObject(g3,g6)
    c: PointOnObject(g4,g6)
    c: PointOnObject(g5,g6)
    c: Coincident(g6,g-1)
    c: PointOnObject(g0,g-2)
    c: DistanceX(g1,g0) = 1.54
FEATURE [PartDesign::Pocket] Pocket470  label="M3x8 Wrench060"
  BaseFeature = -> Pad506
  Length = 1
  Length2 = 100
  Profile = -> Sketch1140
  Type = 0
FEATURE [PartDesign::Pad] Pad523  label="M3 Nut Primitive103"
  Length = 1.2
  Length2 = 1.2
  Profile = -> Sketch1284
  Type = 4
FEATURE [Sketcher::SketchObject] Sketch1294
  ExternalGeometry = -> [Pad523]
  MapMode = 5
  Placement = pos=(0,0,0) rot=(0.57735,0.57735,0.57735;2.0944rad)
  Support = -> [YZ_Plane489]
  sketch-geometry (6):
    g0: LineSegment StartX=-2.67543 StartY=1.2 StartZ=0 EndX=-3.67543 EndY=1.2 EndZ=0
    g1: LineSegment StartX=-3.67543 StartY=1.2 StartZ=0 EndX=-3.67543 EndY=-1.2 EndZ=0
    g2: LineSegment StartX=-3.67543 StartY=-1.2 StartZ=0 EndX=-2.67543 EndY=-1.2 EndZ=0
    g3: LineSegment StartX=-2.67543 StartY=-1.2 StartZ=0 EndX=-3.17543 EndY=-1 EndZ=0
    g4: LineSegment StartX=-3.17543 StartY=-1 StartZ=0 EndX=-3.17543 EndY=1 EndZ=0
    g5: LineSegment StartX=-3.17543 StartY=1 StartZ=0 EndX=-2.67543 EndY=1.2 EndZ=0
  constraints (15):
    c: Horizontal(g0)
    c: Coincident(g0,g1)
    c: Coincident(g1,g2)
    c: Coincident(g2,g3)
    c: Coincident(g3,g4)
    c: Coincident(g4,g5)
    c: Coincident(g5,g0)
    c: Symmetric(g4,g3,g-1)
    c: Symmetric(g0,g2,g-1)
    c: Symmetric(g1,g0,g-1)
    c: DistanceX(g0,g4) = 0.5
    c: DistanceY(g3,g4) = 2
    c: DistanceY(g1,g0) = 2.4
    c: PointOnObject(g3,g-3)
    c: DistanceX(g4,g0) = 0.5
FEATURE [PartDesign::Groove] Groove109  label="Halfspherical Shape002"
  Angle = 360
  Axis = (0,-1,7e-16)
  Base = (0,0,-6.9577e-12)
  BaseFeature = -> Pad520
  Placement = pos=(0,0,0) rot=(1,0,0;1.5708rad)
  Profile = -> Sketch1338
  ReferenceAxis = -> Sketch1338 [V_Axis]
  Reversed = true
FEATURE [PartDesign::SubtractivePipe] SubtractivePipe012  label="Horizontal Profile002"
  AuxilleryCurvelinear = true
  AuxillerySpineTangent = false
  BaseFeature = -> Groove109
  Binormal = (0,0,0)
  Mode = 0
  Placement = pos=(0,0,0) rot=(1,0,0;1.5708rad)
  Profile = -> Sketch1163
  Spine = -> Groove109 [Edge2,Edge1]
  SpineTangent = false
  Transformation = 0
  Transition = 0
FEATURE [PartDesign::PolarPattern] PolarPattern002  label="Horizontal Profile Polar Pattern002"
  Angle = 180
  Axis = -> Sketch1163 [N_Axis]
  BaseFeature = -> SubtractivePipe012
  Occurrences = 12
  Originals = -> [SubtractivePipe012]
  Placement = pos=(0,0,0) rot=(1,0,0;1.5708rad)
  Reversed = true
FEATURE [PartDesign::Groove] Groove105  label="Vertical Profiles002"
  Angle = 360
  Axis = (0,1,0)
  Base = (0,0,0)
  BaseFeature = -> PolarPattern002
  Placement = pos=(0,0,0) rot=(1,0,0;1.5708rad)
  Profile = -> Sketch1352
  ReferenceAxis = -> Sketch1352 [V_Axis]
FEATURE [PartDesign::Pad] Pad524  label="M3x8 Head063"
  Length = 2
  Length2 = 100
  Profile = -> Sketch1155
  Type = 0
FEATURE [Sketcher::SketchObject] Sketch1152
  MapMode = 5
  Placement = pos=(0,0,2) rot=(0,0,1;0rad)
  Support = -> [Pad524]
  sketch-geometry (1):
    g0: Circle CenterX=0 CenterY=0 CenterZ=0 NormalX=0 NormalY=0 NormalZ=1 AngleXU=0 Radius=1
  constraints (2):
    c: Coincident(g0,g-1)
    c: Radius(g0) = 1
FEATURE [PartDesign::Pad] Pad509  label="M3x8 Thread060"
  BaseFeature = -> Pad524
  Length = 8
  Length2 = 100
  Profile = -> Sketch1152
  Type = 0
FEATURE [Sketcher::SketchObject] Sketch1164
  MapMode = 5
  Placement = pos=(0,0,0) rot=(1,0,0;3.14159rad)
  Support = -> [Pad509]
  sketch-geometry (7):
    g0: LineSegment StartX=0.77 StartY=0.44456 StartZ=0 EndX=0 EndY=0.889119 EndZ=0
    g1: LineSegment StartX=0 StartY=0.889119 StartZ=0 EndX=-0.77 EndY=0.44456 EndZ=0
    g2: LineSegment StartX=-0.77 StartY=0.44456 StartZ=0 EndX=-0.77 EndY=-0.44456 EndZ=0
    g3: LineSegment StartX=-0.77 StartY=-0.44456 StartZ=0 EndX=3.85628e-11 EndY=-0.889119 EndZ=0
    g4: LineSegment StartX=3.85628e-11 StartY=-0.889119 StartZ=0 EndX=0.77 EndY=-0.44456 EndZ=0
    g5: LineSegment StartX=0.77 StartY=-0.44456 StartZ=0 EndX=0.77 EndY=0.44456 EndZ=0
    g6: Circle [constr] CenterX=0 CenterY=0 CenterZ=0 NormalX=0 NormalY=0 NormalZ=1 AngleXU=0 Radius=0.889119
  constraints (16):
    c: Coincident(g0,g1)
    c: Coincident(g1,g2)
    c: Coincident(g2,g3)
    c: Coincident(g3,g4)
    c: Coincident(g4,g5)
    c: Coincident(g5,g0)
    c: Equal(g0, g1-g5) x5
    c: PointOnObject(g0,g6)
    c: PointOnObject(g1,g6)
    c: PointOnObject(g2,g6)
    c: PointOnObject(g3,g6)
    c: PointOnObject(g4,g6)
    c: PointOnObject(g5,g6)
    c: Coincident(g6,g-1)
    c: PointOnObject(g0,g-2)
    c: DistanceX(g1,g0) = 1.54
FEATURE [PartDesign::Pocket] Pocket466  label="M3x8 Wrench057"
  BaseFeature = -> Pad509
  Length = 1
  Length2 = 100
  Profile = -> Sketch1164
  Type = 0
FEATURE [PartDesign::Pad] Pad525  label="M3 Nut Primitive104"
  Length = 1.2
  Length2 = 1.2
  Profile = -> Sketch1285
  Type = 4
FEATURE [Sketcher::SketchObject] Sketch1287
  ExternalGeometry = -> [Pad525]
  MapMode = 5
  Placement = pos=(0,0,0) rot=(0.57735,0.57735,0.57735;2.0944rad)
  Support = -> [YZ_Plane486]
  sketch-geometry (6):
    g0: LineSegment StartX=-2.67543 StartY=1.2 StartZ=0 EndX=-3.67543 EndY=1.2 EndZ=0
    g1: LineSegment StartX=-3.67543 StartY=1.2 StartZ=0 EndX=-3.67543 EndY=-1.2 EndZ=0
    g2: LineSegment StartX=-3.67543 StartY=-1.2 StartZ=0 EndX=-2.67543 EndY=-1.2 EndZ=0
    g3: LineSegment StartX=-2.67543 StartY=-1.2 StartZ=0 EndX=-3.17543 EndY=-1 EndZ=0
    g4: LineSegment StartX=-3.17543 StartY=-1 StartZ=0 EndX=-3.17543 EndY=1 EndZ=0
    g5: LineSegment StartX=-3.17543 StartY=1 StartZ=0 EndX=-2.67543 EndY=1.2 EndZ=0
  constraints (15):
    c: Horizontal(g0)
    c: Coincident(g0,g1)
    c: Coincident(g1,g2)
    c: Coincident(g2,g3)
    c: Coincident(g3,g4)
    c: Coincident(g4,g5)
    c: Coincident(g5,g0)
    c: Symmetric(g4,g3,g-1)
    c: Symmetric(g0,g2,g-1)
    c: Symmetric(g1,g0,g-1)
    c: DistanceX(g0,g4) = 0.5
    c: DistanceY(g3,g4) = 2
    c: DistanceY(g1,g0) = 2.4
    c: PointOnObject(g3,g-3)
    c: DistanceX(g4,g0) = 0.5
FEATURE [PartDesign::Groove] Groove108  label="M3 Nut Smooth103"
  Angle = 360
  Axis = (-2e-16,3e-16,1)
  Base = (0,0,0)
  BaseFeature = -> Pad525
  Profile = -> Sketch1287
  ReferenceAxis = -> Sketch1287 [V_Axis]
  Reversed = true
FEATURE [PartDesign::Pocket] Pocket481  label="M3x8 Wrench062"
  BaseFeature = -> Pad519
  Length = 1
  Length2 = 100
  Profile = -> Sketch1167
  Type = 0
FEATURE [PartDesign::Pad] Pad526  label="Baseplate025"
  Length = 20
  Length2 = 100
  Profile = -> Sketch1337
  Type = 0
FEATURE [Sketcher::SketchObject] Sketch1344
  ExternalGeometry = -> [Pad526]
  MapMode = 5
  Placement = pos=(0,0,20) rot=(0,0,1;0rad)
  Support = -> [Pad526]
  sketch-geometry (18):
    g0: LineSegment StartX=-87.0711 StartY=22.0711 StartZ=0 EndX=-72.9287 EndY=7.92875 EndZ=0
    g1: LineSegment StartX=-50 StartY=17.1099 StartZ=0 EndX=-30 EndY=17.1099 EndZ=0
    g2: LineSegment StartX=-30 StartY=17.1099 StartZ=0 EndX=-30 EndY=25 EndZ=0
    g3: LineSegment StartX=-30 StartY=25 StartZ=0 EndX=-50 EndY=25 EndZ=0
    g4: LineSegment StartX=-50 StartY=25 StartZ=0 EndX=-50 EndY=17.1099 EndZ=0
    g5: LineSegment StartX=-55 StartY=25 StartZ=0 EndX=-55 EndY=17.1099 EndZ=0
    g6: LineSegment StartX=-55 StartY=25 StartZ=0 EndX=-80 EndY=25 EndZ=0
    g7: LineSegment StartX=-25 StartY=25 StartZ=0 EndX=-25 EndY=17.1099 EndZ=0
    g8: ArcOfCircle CenterX=-80 CenterY=15 CenterZ=0 NormalX=0 NormalY=0 NormalZ=1 AngleXU=0 Radius=10 StartAngle=1.5708 EndAngle=2.35619
    g9: ArcOfCircle CenterX=-50 CenterY=-14.75 CenterZ=0 NormalX=0 NormalY=0 NormalZ=1 AngleXU=0 Radius=32.2499 StartAngle=1.72646 EndAngle=2.36168
    g10: ArcOfCircle CenterX=-30 CenterY=-14.75 CenterZ=0 NormalX=0 NormalY=0 NormalZ=1 AngleXU=0 Radius=32.2499 StartAngle=0.781214 EndAngle=1.41513
    g11: ArcOfCircle CenterX=0 CenterY=15 CenterZ=0 NormalX=0 NormalY=0 NormalZ=1 AngleXU=0 Radius=10.0001 StartAngle=3.92281 EndAngle=4.1888
    g12: LineSegment StartX=-25 StartY=25 StartZ=0 EndX=-5 EndY=25 EndZ=0
    g13: LineSegment StartX=-5 StartY=25 StartZ=0 EndX=-5 EndY=6.33958 EndZ=0
    g14: LineSegment StartX=8 StartY=25 StartZ=0 EndX=48.5 EndY=25 EndZ=0
    g15: LineSegment StartX=48.5 StartY=25 StartZ=0 EndX=48.5 EndY=5 EndZ=0
    g16: LineSegment StartX=48.5 StartY=5 StartZ=0 EndX=8 EndY=5 EndZ=0
    g17: LineSegment StartX=8 StartY=5 StartZ=0 EndX=8 EndY=25 EndZ=0
  constraints (52):
    c: Coincident(g1,g2)
    c: Coincident(g2,g3)
    c: Coincident(g3,g4)
    c: Coincident(g4,g1)
    c: Horizontal(g1)
    c: Horizontal(g3)
    c: Vertical(g2)
    c: Vertical(g4)
    c: Coincident(g6,g5)
    c: Horizontal(g6)
    c: Vertical(g7)
    c: Vertical(g5)
    c: Coincident(g8,g0)
    c: Coincident(g9,g5)
    c: Coincident(g10,g7)
    c: Coincident(g12,g7)
    c: Horizontal(g12)
    c: Tangent(g8,g6) = -1.5708
    c: Horizontal(g5,g3)
    c: Horizontal(g2,g7)
    c: Horizontal(g1,g7)
    c: Horizontal(g5,g1)
    c: Tangent(g11,g10) = 1.5708
    c: Angle(g0) = -0.785398
    c: Radius(g8) = 10
    c: Coincident(g8,g-3)
    c: PointOnObject(g8,g0)
    c: Coincident(g9,g0)
    c: DistanceX(g5,g3) = 5
    c: DistanceX(g2,g7) = 5
    c: DistanceX(g11,g-1) = 5
    c: Coincident(g13,g12)
    c: Coincident(g13,g11)
    c: Vertical(g13)
    c: Coincident(g-4,g9)
    c: Coincident(g10,g-5)
    c: Distance(g0,g-4) = 5
    c: Coincident(g11,g-6)
    c: Vertical(g-4,g1)
    c: Vertical(g-5,g1)
    c: Coincident(g14,g15)
    c: Coincident(g15,g16)
    c: Coincident(g16,g17)
    c: Coincident(g17,g14)
    c: Horizontal(g14)
    c: Horizontal(g16)
    c: Vertical(g15)
    c: Vertical(g17)
    c: DistanceX(g-1,g16) = 8
    c: DistanceY(g-1,g16) = 5
    c: DistanceX(g14,g14) = 40.5
    c: DistanceY(g15,g15) = 20
FEATURE [PartDesign::Pocket] Pocket483  label="Cut Sides002"
  BaseFeature = -> Groove105
  Length = 25
  Length2 = 100
  Placement = pos=(0,0,0) rot=(1,0,0;1.5708rad)
  Profile = -> Sketch1278
  Reversed = true
  Type = 0
FEATURE [PartDesign::Pocket] Pocket479  label="Inner Halfspherical Cutout002"
  BaseFeature = -> Pocket483
  Length = 10
  Length2 = 10
  Placement = pos=(0,0,0) rot=(1,0,0;1.5708rad)
  Profile = -> Sketch1358
  Type = 4
FEATURE [PartDesign::Pocket] Pocket472  label="Slanted Edge002"
  BaseFeature = -> Pocket479
  Length = 15
  Length2 = 15
  Placement = pos=(0,0,0) rot=(1,0,0;1.5708rad)
  Profile = -> Sketch1353
  Type = 4
FEATURE [PartDesign::Pad] Pad528  label="M3 Nut Primitive105"
  Length = 0.6
  Length2 = 0.6
  Profile = -> Sketch1142
  Type = 4
FEATURE [Sketcher::SketchObject] Sketch1307
  ExternalGeometry = -> [Pad528]
  MapMode = 5
  Placement = pos=(0,0,0) rot=(0.57735,0.57735,0.57735;2.0944rad)
  Support = -> [YZ_Plane568]
  sketch-geometry (6):
    g0: LineSegment StartX=-1.9594 StartY=0.6 StartZ=0 EndX=-2.8094 EndY=0.6 EndZ=0
    g1: LineSegment StartX=-2.8094 StartY=0.6 StartZ=0 EndX=-2.8094 EndY=-0.6 EndZ=0
    g2: LineSegment StartX=-2.8094 StartY=-0.6 StartZ=0 EndX=-1.9594 EndY=-0.6 EndZ=0
    g3: LineSegment StartX=-1.9594 StartY=-0.6 StartZ=0 EndX=-2.3094 EndY=-0.4 EndZ=0
    g4: LineSegment StartX=-2.3094 StartY=-0.4 StartZ=0 EndX=-2.3094 EndY=0.4 EndZ=0
    g5: LineSegment StartX=-2.3094 StartY=0.4 StartZ=0 EndX=-1.9594 EndY=0.6 EndZ=0
  constraints (15):
    c: Horizontal(g0)
    c: Coincident(g0,g1)
    c: Coincident(g1,g2)
    c: Coincident(g2,g3)
    c: Coincident(g3,g4)
    c: Coincident(g4,g5)
    c: Coincident(g5,g0)
    c: Symmetric(g4,g3,g-1)
    c: Symmetric(g0,g2,g-1)
    c: Symmetric(g1,g0,g-1)
    c: DistanceX(g0,g4) = 0.5
    c: DistanceY(g3,g4) = 0.8
    c: DistanceY(g1,g0) = 1.2
    c: PointOnObject(g3,g-3)
    c: DistanceX(g4,g0) = 0.35
FEATURE [PartDesign::Groove] Groove107  label="M3 Nut Smooth102"
  Angle = 360
  Axis = (-2e-16,3e-16,1)
  Base = (0,0,0)
  BaseFeature = -> Pad528
  Profile = -> Sketch1307
  ReferenceAxis = -> Sketch1307 [V_Axis]
  Reversed = true
FEATURE [PartDesign::Pad] Pad529  label="M3 Nut Primitive106"
  Length = 0.6
  Length2 = 0.6
  Profile = -> Sketch1291
  Type = 4
FEATURE [Sketcher::SketchObject] Sketch1273
  ExternalGeometry = -> [Pad529]
  MapMode = 5
  Placement = pos=(0,0,0) rot=(0.57735,0.57735,0.57735;2.0944rad)
  Support = -> [YZ_Plane484]
  sketch-geometry (6):
    g0: LineSegment StartX=-1.9594 StartY=0.6 StartZ=0 EndX=-2.8094 EndY=0.6 EndZ=0
    g1: LineSegment StartX=-2.8094 StartY=0.6 StartZ=0 EndX=-2.8094 EndY=-0.6 EndZ=0
    g2: LineSegment StartX=-2.8094 StartY=-0.6 StartZ=0 EndX=-1.9594 EndY=-0.6 EndZ=0
    g3: LineSegment StartX=-1.9594 StartY=-0.6 StartZ=0 EndX=-2.3094 EndY=-0.4 EndZ=0
    g4: LineSegment StartX=-2.3094 StartY=-0.4 StartZ=0 EndX=-2.3094 EndY=0.4 EndZ=0
    g5: LineSegment StartX=-2.3094 StartY=0.4 StartZ=0 EndX=-1.9594 EndY=0.6 EndZ=0
  constraints (15):
    c: Horizontal(g0)
    c: Coincident(g0,g1)
    c: Coincident(g1,g2)
    c: Coincident(g2,g3)
    c: Coincident(g3,g4)
    c: Coincident(g4,g5)
    c: Coincident(g5,g0)
    c: Symmetric(g4,g3,g-1)
    c: Symmetric(g0,g2,g-1)
    c: Symmetric(g1,g0,g-1)
    c: DistanceX(g0,g4) = 0.5
    c: DistanceY(g3,g4) = 0.8
    c: DistanceY(g1,g0) = 1.2
    c: PointOnObject(g3,g-3)
    c: DistanceX(g4,g0) = 0.35
FEATURE [PartDesign::Groove] Groove106  label="M3 Nut Smooth101"
  Angle = 360
  Axis = (-2e-16,3e-16,1)
  Base = (0,0,0)
  BaseFeature = -> Pad529
  Profile = -> Sketch1273
  ReferenceAxis = -> Sketch1273 [V_Axis]
  Reversed = true
FEATURE [PartDesign::Chamfer] Chamfer241  label="M3 Nut Smooth Hole101"
  Base = -> Groove106 [Edge24,Edge23]
  BaseFeature = -> Groove106
  Size = 0.2
FEATURE [PartDesign::Body] Body302  label="M2 Nut042"
  Group = -> [Sketch1291,Pad529,Sketch1273,Groove106,Chamfer241]
  Origin = -> Origin466
  Placement = pos=(-115.141,-152.75,71.5896) rot=(0.677661,0.519988,-0.519988;1.95044rad)
  Tip = -> Chamfer241
FEATURE [PartDesign::Pad] Pad530  label="M3x8 Head064"
  Length = 3
  Length2 = 100
  Profile = -> Sketch1366
  Type = 0
FEATURE [Sketcher::SketchObject] Sketch1355
  MapMode = 5
  Placement = pos=(0,0,3) rot=(0,0,1;0rad)
  Support = -> [Pad530]
  sketch-geometry (1):
    g0: Circle CenterX=0 CenterY=0 CenterZ=0 NormalX=0 NormalY=0 NormalZ=1 AngleXU=0 Radius=1.5
  constraints (2):
    c: Coincident(g0,g-1)
    c: Radius(g0) = 1.5
FEATURE [PartDesign::Pad] Pad531  label="Ball Bearing Pin004"
  Length = 5
  Length2 = 100
  Profile = -> Sketch1331
  Type = 0
FEATURE [PartDesign::Groove] Groove111  label="M3 Nut Smooth105"
  Angle = 360
  Axis = (-2e-16,3e-16,1)
  Base = (0,0,0)
  BaseFeature = -> Pad518
  Profile = -> Sketch1364
  ReferenceAxis = -> Sketch1364 [V_Axis]
  Reversed = true
FEATURE [PartDesign::Chamfer] Chamfer237  label="M3 Nut Smooth Hole100"
  Base = -> Groove111 [Edge24,Edge23]
  BaseFeature = -> Groove111
  Size = 0.2
FEATURE [PartDesign::Body] Body350  label="M3 Nut064"
  Group = -> [Sketch1359,Pad518,Sketch1364,Groove111,Chamfer237]
  Origin = -> Origin480
  Placement = pos=(0.75,-5.5,34.25) rot=(1,0,0;1.5708rad)
  Tip = -> Chamfer237
FEATURE [PartDesign::Pad] Pad532  label="Baseplate026"
  Length = 25
  Length2 = 100
  Profile = -> Sketch1277
  Type = 0
FEATURE [Sketcher::SketchObject] Sketch1288
  MapMode = 5
  Placement = pos=(0,0,25) rot=(0,0,1;0rad)
  Support = -> [Pad532]
  sketch-geometry (4):
    g0: LineSegment StartX=8 StartY=0 StartZ=0 EndX=48.5 EndY=0 EndZ=0
    g1: LineSegment StartX=48.5 StartY=0 StartZ=0 EndX=48.5 EndY=-19 EndZ=0
    g2: LineSegment StartX=48.5 StartY=-19 StartZ=0 EndX=8 EndY=-19 EndZ=0
    g3: LineSegment StartX=8 StartY=-19 StartZ=0 EndX=8 EndY=0 EndZ=0
  constraints (12):
    c: Coincident(g0,g1)
    c: Coincident(g1,g2)
    c: Coincident(g2,g3)
    c: Coincident(g3,g0)
    c: Horizontal(g0)
    c: Horizontal(g2)
    c: Vertical(g1)
    c: Vertical(g3)
    c: PointOnObject(g0,g-1)
    c: DistanceY(g3,g3) = 19
    c: DistanceX(g0,g0) = 40.5
    c: DistanceX(g-1,g0) = 8
FEATURE [PartDesign::Pad] Pad533  label="M3x8 Thread063"
  BaseFeature = -> Pad516
  Length = 8
  Length2 = 100
  Profile = -> Sketch1272
  Type = 0
FEATURE [Sketcher::SketchObject] Sketch1289
  MapMode = 5
  Placement = pos=(0,0,0) rot=(1,0,0;3.14159rad)
  Support = -> [Pad533]
  sketch-geometry (7):
    g0: LineSegment StartX=0.77 StartY=0.44456 StartZ=0 EndX=0 EndY=0.889119 EndZ=0
    g1: LineSegment StartX=0 StartY=0.889119 StartZ=0 EndX=-0.77 EndY=0.44456 EndZ=0
    g2: LineSegment StartX=-0.77 StartY=0.44456 StartZ=0 EndX=-0.77 EndY=-0.44456 EndZ=0
    g3: LineSegment StartX=-0.77 StartY=-0.44456 StartZ=0 EndX=3.85628e-11 EndY=-0.889119 EndZ=0
    g4: LineSegment StartX=3.85628e-11 StartY=-0.889119 StartZ=0 EndX=0.77 EndY=-0.44456 EndZ=0
    g5: LineSegment StartX=0.77 StartY=-0.44456 StartZ=0 EndX=0.77 EndY=0.44456 EndZ=0
    g6: Circle [constr] CenterX=0 CenterY=0 CenterZ=0 NormalX=0 NormalY=0 NormalZ=1 AngleXU=0 Radius=0.889119
  constraints (16):
    c: Coincident(g0,g1)
    c: Coincident(g1,g2)
    c: Coincident(g2,g3)
    c: Coincident(g3,g4)
    c: Coincident(g4,g5)
    c: Coincident(g5,g0)
    c: Equal(g0, g1-g5) x5
    c: PointOnObject(g0,g6)
    c: PointOnObject(g1,g6)
    c: PointOnObject(g2,g6)
    c: PointOnObject(g3,g6)
    c: PointOnObject(g4,g6)
    c: PointOnObject(g5,g6)
    c: Coincident(g6,g-1)
    c: PointOnObject(g0,g-2)
    c: DistanceX(g1,g0) = 1.54
FEATURE [PartDesign::Pocket] Pocket490  label="M3x8 Wrench063"
  BaseFeature = -> Pad533
  Length = 1
  Length2 = 100
  Profile = -> Sketch1289
  Type = 0
FEATURE [PartDesign::Pad] Pad534  label="M3x20 Head040"
  Length = 3
  Length2 = 100
  Profile = -> Sketch1318
  Type = 0
FEATURE [Sketcher::SketchObject] Sketch1334
  MapMode = 5
  Placement = pos=(0,0,3) rot=(0,0,1;0rad)
  Support = -> [Pad534]
  sketch-geometry (1):
    g0: Circle CenterX=0 CenterY=0 CenterZ=0 NormalX=0 NormalY=0 NormalZ=1 AngleXU=0 Radius=1.5
  constraints (2):
    c: Coincident(g0,g-1)
    c: Radius(g0) = 1.5
FEATURE [PartDesign::Pad] Pad535  label="M3x20 Head041"
  Length = 3
  Length2 = 100
  Profile = -> Sketch1173
  Type = 0
FEATURE [Sketcher::SketchObject] Sketch1325
  MapMode = 5
  Placement = pos=(0,0,3) rot=(0,0,1;0rad)
  Support = -> [Pad535]
  sketch-geometry (1):
    g0: Circle CenterX=0 CenterY=0 CenterZ=0 NormalX=0 NormalY=0 NormalZ=1 AngleXU=0 Radius=1.5
  constraints (2):
    c: Coincident(g0,g-1)
    c: Radius(g0) = 1.5
FEATURE [PartDesign::Pad] Pad536  label="M3x20 Head042"
  Length = 3
  Length2 = 100
  Profile = -> Sketch1324
  Type = 0
FEATURE [Sketcher::SketchObject] Sketch1165
  MapMode = 5
  Placement = pos=(0,0,3) rot=(0,0,1;0rad)
  Support = -> [Pad536]
  sketch-geometry (1):
    g0: Circle CenterX=0 CenterY=0 CenterZ=0 NormalX=0 NormalY=0 NormalZ=1 AngleXU=0 Radius=1.5
  constraints (2):
    c: Coincident(g0,g-1)
    c: Radius(g0) = 1.5
FEATURE [PartDesign::Pad] Pad522  label="M3x20 Thread040"
  BaseFeature = -> Pad536
  Length = 20
  Length2 = 100
  Profile = -> Sketch1165
  Type = 0
FEATURE [Sketcher::SketchObject] Sketch1162
  MapMode = 5
  Placement = pos=(0,0,0) rot=(1,0,0;3.14159rad)
  Support = -> [Pad522]
  sketch-geometry (7):
    g0: LineSegment StartX=1.275 StartY=0.736122 StartZ=0 EndX=0 EndY=1.47224 EndZ=0
    g1: LineSegment StartX=0 StartY=1.47224 StartZ=0 EndX=-1.275 EndY=0.736122 EndZ=0
    g2: LineSegment StartX=-1.275 StartY=0.736122 StartZ=0 EndX=-1.275 EndY=-0.736122 EndZ=0
    g3: LineSegment StartX=-1.275 StartY=-0.736122 StartZ=0 EndX=1.34766e-11 EndY=-1.47224 EndZ=0
    g4: LineSegment StartX=1.34766e-11 StartY=-1.47224 StartZ=0 EndX=1.275 EndY=-0.736122 EndZ=0
    g5: LineSegment StartX=1.275 StartY=-0.736122 StartZ=0 EndX=1.275 EndY=0.736122 EndZ=0
    g6: Circle [constr] CenterX=0 CenterY=0 CenterZ=0 NormalX=0 NormalY=0 NormalZ=1 AngleXU=0 Radius=1.47224
  constraints (16):
    c: Coincident(g0,g1)
    c: Coincident(g1,g2)
    c: Coincident(g2,g3)
    c: Coincident(g3,g4)
    c: Coincident(g4,g5)
    c: Coincident(g5,g0)
    c: Equal(g0, g1-g5) x5
    c: PointOnObject(g0,g6)
    c: PointOnObject(g1,g6)
    c: PointOnObject(g2,g6)
    c: PointOnObject(g3,g6)
    c: PointOnObject(g4,g6)
    c: PointOnObject(g5,g6)
    c: Coincident(g6,g-1)
    c: PointOnObject(g0,g-2)
    c: DistanceX(g1,g0) = 2.55
FEATURE [PartDesign::Pocket] Pocket482  label="M3x20 Wrench040"
  BaseFeature = -> Pad522
  Length = 1.3
  Length2 = 100
  Profile = -> Sketch1162
  Type = 0
FEATURE [PartDesign::Groove] Groove112  label="M3 Nut Smooth106"
  Angle = 360
  Axis = (-2e-16,3e-16,1)
  Base = (0,0,0)
  BaseFeature = -> Pad523
  Profile = -> Sketch1294
  ReferenceAxis = -> Sketch1294 [V_Axis]
  Reversed = true
FEATURE [PartDesign::Pocket] Pocket494  label="Leg and Servo Pockets002"
  BaseFeature = -> Pad526
  Length = 20
  Length2 = 100
  Profile = -> Sketch1344
  Type = 0
FEATURE [PartDesign::Fillet] Fillet156  label="Smooth Leg Pockets002"
  Base = -> Pocket494 [Edge76,Edge72,Edge73,Edge75,Edge69,Edge70,Edge71,Edge68,Edge77,Edge81,Edge79,Edge80]
  BaseFeature = -> Pocket494
  Radius = 2
FEATURE [Sketcher::SketchObject] Sketch1171
  MapMode = 5
  Placement = pos=(0,0,20) rot=(0,0,1;0rad)
  Support = -> [Fillet156]
  sketch-geometry (4):
    g0: LineSegment StartX=0 StartY=0 StartZ=0 EndX=56.5 EndY=0 EndZ=0
    g1: LineSegment StartX=56.5 StartY=0 StartZ=0 EndX=56.5 EndY=25 EndZ=0
    g2: LineSegment StartX=56.5 StartY=25 StartZ=0 EndX=0 EndY=25 EndZ=0
    g3: LineSegment StartX=0 StartY=25 StartZ=0 EndX=0 EndY=0 EndZ=0
  constraints (11):
    c: Coincident(g0,g1)
    c: Coincident(g1,g2)
    c: Coincident(g2,g3)
    c: Coincident(g3,g0)
    c: Horizontal(g0)
    c: Horizontal(g2)
    c: Vertical(g1)
    c: Vertical(g3)
    c: Coincident(g0,g-1)
    c: DistanceY(g3,g3) = 25
    c: DistanceX(g2,g2) = 56.5
FEATURE [PartDesign::Pocket] Pocket471  label="Counterpart Pocket002"
  BaseFeature = -> Fillet156
  Length = 10
  Length2 = 100
  Profile = -> Sketch1171
  Type = 0
FEATURE [PartDesign::Pad] Pad527  label="Extend Baseplate002"
  BaseFeature = -> Pocket471
  Length = 12
  Length2 = 100
  Profile = -> Pocket471 [Face40]
  Type = 0
FEATURE [Sketcher::SketchObject] Sketch1351
  MapMode = 5
  Placement = pos=(0,0,32) rot=(0,0,1;0rad)
  Support = -> [Pad527]
  sketch-geometry (4):
    g0: LineSegment StartX=48.5 StartY=25 StartZ=0 EndX=56.5 EndY=25 EndZ=0
    g1: LineSegment StartX=56.5 StartY=25 StartZ=0 EndX=56.5 EndY=30 EndZ=0
    g2: LineSegment StartX=56.5 StartY=30 StartZ=0 EndX=48.5 EndY=30 EndZ=0
    g3: LineSegment StartX=48.5 StartY=30 StartZ=0 EndX=48.5 EndY=25 EndZ=0
  constraints (12):
    c: Coincident(g0,g1)
    c: Coincident(g1,g2)
    c: Coincident(g2,g3)
    c: Coincident(g3,g0)
    c: Horizontal(g0)
    c: Horizontal(g2)
    c: Vertical(g1)
    c: Vertical(g3)
    c: DistanceY(g3,g3) = 5
    c: DistanceY(g-1,g0) = 25
    c: DistanceX(g2,g2) = 8
    c: DistanceX(g-1,g2) = 48.5
FEATURE [PartDesign::Pocket] Pocket478  label="Remove Extension Servocover002"
  BaseFeature = -> Pad527
  Length = 13
  Length2 = 100
  Profile = -> Sketch1351
  Type = 0
FEATURE [Sketcher::SketchObject] Sketch1345
  MapMode = 5
  Placement = pos=(0,30,0) rot=(0,0.707107,0.707107;3.14159rad)
  Support = -> [Pocket478]
  sketch-geometry (7):
    g0: ArcOfCircle CenterX=22.5 CenterY=65.1875 CenterZ=0 NormalX=0 NormalY=0 NormalZ=1 AngleXU=0 Radius=45.1875 StartAngle=4.19118 EndAngle=4.71239
    g1: LineSegment StartX=-56.5 StartY=33 StartZ=0 EndX=95 EndY=33 EndZ=0
    g2: LineSegment StartX=95 StartY=33 StartZ=0 EndX=95 EndY=20 EndZ=0
    g3: LineSegment StartX=95 StartY=20 StartZ=0 EndX=22.5 EndY=20 EndZ=0
    g4: ArcOfCircle CenterX=-22.5 CenterY=-13.1875 CenterZ=0 NormalX=0 NormalY=0 NormalZ=1 AngleXU=0 Radius=45.1875 StartAngle=1.04959 EndAngle=1.5708
    g5: LineSegment StartX=-22.5 StartY=32 StartZ=0 EndX=-56.5 EndY=32 EndZ=0
    g6: LineSegment StartX=-56.5 StartY=32 StartZ=0 EndX=-56.5 EndY=33 EndZ=0
  constraints (21):
    c: Horizontal(g1)
    c: Coincident(g2,g1)
    c: Vertical(g2)
    c: Coincident(g3,g2)
    c: Horizontal(g3)
    c: Tangent(g3,g0) = 1.5708
    c: DistanceX(g0,g0) = 22.5
    c: DistanceY(g0,g1) = 7
    c: DistanceY(g2,g2) = 13
    c: PointOnObject(g0,g-2)
    c: DistanceY(g-1,g2) = 20
    c: Tangent(g4,g0) = 1.5708
    c: Horizontal(g5)
    c: Coincident(g6,g5)
    c: Coincident(g1,g6)
    c: Vertical(g6)
    c: Tangent(g5,g4) = -1.5708
    c: DistanceY(g6,g6) = 1
    c: DistanceX(g5,g0) = 56.5
    c: DistanceX(g0,g1) = 95
    c: DistanceX(g4,g0) = 22.5
FEATURE [PartDesign::Pocket] Pocket484  label="Swing Leg002"
  BaseFeature = -> Pocket478
  Length = 35
  Length2 = 100
  Profile = -> Sketch1345
  Type = 0
FEATURE [PartDesign::Fillet] Fillet147  label="Servocable 002"
  Base = -> Pocket484 [Edge144,Edge135]
  BaseFeature = -> Pocket484
  Radius = 3
FEATURE [Sketcher::SketchObject] Sketch1336
  ExternalGeometry = -> [Fillet147]
  MapMode = 5
  Placement = pos=(0,4.4e-15,20) rot=(0,0,1;0rad)
  Support = -> [Fillet147]
  sketch-geometry (12):
    g0: Circle CenterX=-25.3678 CenterY=16.4091 CenterZ=0 NormalX=0 NormalY=0 NormalZ=1 AngleXU=0 Radius=1.6
    g1: LineSegment [constr] StartX=-23 StartY=18.7769 StartZ=0 EndX=-26.2345 EndY=19.6436 EndZ=0
    g2: LineSegment [constr] StartX=-26.2345 StartY=19.6436 StartZ=0 EndX=-28.6024 EndY=17.2757 EndZ=0
    g3: LineSegment [constr] StartX=-28.6024 StartY=17.2757 StartZ=0 EndX=-27.7357 EndY=14.0412 EndZ=0
    g4: LineSegment [constr] StartX=-27.7357 StartY=14.0412 StartZ=0 EndX=-24.5012 EndY=13.1745 EndZ=0
    g5: LineSegment [constr] StartX=-24.5012 StartY=13.1745 StartZ=0 EndX=-22.1333 EndY=15.5424 EndZ=0
    g6: LineSegment [constr] StartX=-22.1333 StartY=15.5424 StartZ=0 EndX=-23 EndY=18.7769 EndZ=0
    g7: Circle [constr] CenterX=-25.3678 CenterY=16.4091 CenterZ=0 NormalX=0 NormalY=0 NormalZ=1 AngleXU=0 Radius=3.34863
    g8: Circle CenterX=4 CenterY=20 CenterZ=0 NormalX=0 NormalY=0 NormalZ=1 AngleXU=0 Radius=1.6
    g9: Circle CenterX=52.5 CenterY=20 CenterZ=0 NormalX=0 NormalY=0 NormalZ=1 AngleXU=0 Radius=1.6
    g10: Circle CenterX=52.5 CenterY=10 CenterZ=0 NormalX=0 NormalY=0 NormalZ=1 AngleXU=0 Radius=1.6
    g11: Circle CenterX=4 CenterY=10 CenterZ=0 NormalX=0 NormalY=0 NormalZ=1 AngleXU=0 Radius=1.6
  constraints (30):
    c: Radius(g0) = 1.6
    c: Coincident(g1,g2)
    c: Coincident(g2,g3)
    c: Coincident(g3,g4)
    c: Coincident(g4,g5)
    c: Coincident(g5,g6)
    c: Coincident(g6,g1)
    c: Equal(g1, g2-g6) x5
    c: PointOnObject(g1,g7)
    c: PointOnObject(g2,g7)
    c: PointOnObject(g3,g7)
    c: PointOnObject(g4,g7)
    c: PointOnObject(g5,g7)
    c: PointOnObject(g6,g7)
    c: Coincident(g7,g0)
    c: Distance(g4,g2) = 5.8
    c: Coincident(g1,g-3)
    c: Angle(g5) = 0.785398
    c: Horizontal(g8,g9)
    c: Horizontal(g11,g10)
    c: Vertical(g10,g9)
    c: Vertical(g8,g11)
    c: Equal(g11,g8)
    c: Equal(g8,g9)
    c: Equal(g9,g10)
    c: Equal(g8,g0)
    c: DistanceX(g11,g10) = 48.5
    c: DistanceY(g11,g8) = 10
    c: DistanceY(g-1,g11) = 10
    c: DistanceX(g-1,g11) = 4
FEATURE [PartDesign::Pocket] Pocket477  label="Screwhole002"
  BaseFeature = -> Fillet147
  Length = 20
  Length2 = 100
  Profile = -> Sketch1336
  Type = 0
FEATURE [Sketcher::SketchObject] Sketch1350
  MapMode = 5
  Placement = pos=(0,4.4e-15,20) rot=(0,0,1;0rad)
  Support = -> [Pocket477]
  sketch-geometry (5):
    g0: ArcOfCircle CenterX=-80 CenterY=15 CenterZ=0 NormalX=0 NormalY=0 NormalZ=1 AngleXU=0 Radius=12.5 StartAngle=2.35619 EndAngle=5.49779
    g1: LineSegment [constr] StartX=-88.8388 StartY=23.8388 StartZ=0 EndX=-71.1612 EndY=6.16117 EndZ=0
    g2: LineSegment StartX=-88.8388 StartY=23.8388 StartZ=0 EndX=-92.3744 EndY=27.3744 EndZ=0
    g3: LineSegment StartX=-71.1612 StartY=6.16117 StartZ=0 EndX=-67.6256 EndY=2.62563 EndZ=0
    g4: ArcOfCircle CenterX=-80 CenterY=15 CenterZ=0 NormalX=0 NormalY=0 NormalZ=1 AngleXU=0 Radius=17.5 StartAngle=2.35619 EndAngle=5.49779
  constraints (15):
    c: Radius(g0) = 12.5
    c: DistanceX(g0,g-1) = 80
    c: DistanceY(g-1,g0) = 15
    c: Coincident(g1,g0)
    c: Coincident(g1,g0)
    c: Angle(g1) = -0.785398
    c: PointOnObject(g0,g1)
    c: Coincident(g2,g0)
    c: Coincident(g3,g0)
    c: Coincident(g4,g0)
    c: Coincident(g4,g2)
    c: Coincident(g4,g3)
    c: Tangent(g2,g1)
    c: Tangent(g1,g3)
    c: Radius(g4) = 17.5
FEATURE [PartDesign::Pocket] Pocket473  label="Rubberfoot Pocket002"
  BaseFeature = -> Pocket477
  Length = 20
  Length2 = 100
  Profile = -> Sketch1350
  Type = 0
FEATURE [Sketcher::SketchObject] Sketch1342
  AttachmentOffset = pos=(0,0,-3) rot=(0,0,1;0rad)
  ExternalGeometry = -> [Pocket473]
  MapMode = 5
  Placement = pos=(0,3.7e-15,17) rot=(0,0,1;0rad)
  Support = -> [Pocket473]
  sketch-geometry (10):
    g0: LineSegment [constr] StartX=-52.5747 StartY=33.6444 StartZ=0 EndX=-49.7647 EndY=34.4507 EndZ=0
    g1: LineSegment StartX=-49.7647 StartY=34.4507 StartZ=0 EndX=-52.5747 EndY=33.6444 EndZ=0
    g2: LineSegment StartX=-52.5747 StartY=33.6444 StartZ=0 EndX=-55.0934 EndY=32.1605 EndZ=0
    g3: LineSegment StartX=-55.0934 StartY=32.1605 StartZ=0 EndX=-57.1605 EndY=30.0934 EndZ=0
    g4: LineSegment StartX=-57.1605 StartY=30.0934 StartZ=0 EndX=-55.0934 EndY=32.1605 EndZ=0
    g5: LineSegment [constr] StartX=-55.0934 StartY=32.1605 StartZ=0 EndX=-52.5747 EndY=33.6444 EndZ=0
    g6: Circle [constr] CenterX=-48 CenterY=23 CenterZ=0 NormalX=0 NormalY=0 NormalZ=1 AngleXU=0 Radius=11.5858
    g7: LineSegment StartX=-55.0934 StartY=32.1605 StartZ=0 EndX=-53.6792 EndY=33.5747 EndZ=0
    g8: LineSegment StartX=-53.6792 StartY=33.5747 StartZ=0 EndX=-53.4871 EndY=33.3827 EndZ=0
    g9: LineSegment StartX=-53.4871 StartY=33.3827 StartZ=0 EndX=-49.7647 EndY=34.4507 EndZ=0
  constraints (23):
    c: Coincident(g0,g1)
    c: Coincident(g1,g2)
    c: Coincident(g2,g3)
    c: Coincident(g3,g4)
    c: Coincident(g4,g5)
    c: Coincident(g5,g0)
    c: Equal(g0, g1-g5) x5
    c: PointOnObject(g0,g6)
    c: PointOnObject(g1,g6)
    c: PointOnObject(g2,g6)
    c: PointOnObject(g3,g6)
    c: PointOnObject(g4,g6)
    c: PointOnObject(g5,g6)
    c: Coincident(g6,g-3)
    c: Angle(g4) = 0.785398
    c: Distance(g1,g3) = 5.8
    c: Coincident(g8,g7)
    c: Coincident(g9,g8)
    c: Coincident(g9,g0)
    c: Tangent(g7,g4) = -1.5708
    c: Tangent(g9,g1)
    c: Perpendicular(g8,g7)
    c: Distance(g7) = 2
FEATURE [Sketcher::SketchObject] Sketch1357
  AttachmentOffset = pos=(0,0,-17) rot=(0,0,1;0rad)
  ExternalGeometry = -> [Pocket473]
  MapMode = 5
  Placement = pos=(0,7e-16,3) rot=(0,0,1;0rad)
  Support = -> [Pocket473]
  sketch-geometry (10):
    g0: LineSegment [constr] StartX=-52.5746 StartY=33.6443 StartZ=0 EndX=-49.7646 EndY=34.4505 EndZ=0
    g1: LineSegment StartX=-49.7646 StartY=34.4505 StartZ=0 EndX=-52.5746 EndY=33.6443 EndZ=0
    g2: LineSegment StartX=-52.5746 StartY=33.6443 StartZ=0 EndX=-55.0933 EndY=32.1604 EndZ=0
    g3: LineSegment StartX=-55.0933 StartY=32.1604 StartZ=0 EndX=-57.1604 EndY=30.0933 EndZ=0
    g4: LineSegment StartX=-57.1604 StartY=30.0933 StartZ=0 EndX=-55.0933 EndY=32.1604 EndZ=0
    g5: LineSegment [constr] StartX=-55.0933 StartY=32.1604 StartZ=0 EndX=-52.5746 EndY=33.6443 EndZ=0
    g6: Circle [constr] CenterX=-48 CenterY=23 CenterZ=0 NormalX=0 NormalY=0 NormalZ=1 AngleXU=0 Radius=11.5857
    g7: LineSegment StartX=-55.0933 StartY=32.1604 StartZ=0 EndX=-53.6791 EndY=33.5746 EndZ=0
    g8: LineSegment StartX=-53.6791 StartY=33.5746 StartZ=0 EndX=-53.487 EndY=33.3826 EndZ=0
    g9: LineSegment StartX=-53.487 StartY=33.3826 StartZ=0 EndX=-49.7646 EndY=34.4505 EndZ=0
  constraints (23):
    c: Coincident(g0,g1)
    c: Coincident(g1,g2)
    c: Coincident(g2,g3)
    c: Coincident(g3,g4)
    c: Coincident(g4,g5)
    c: Coincident(g5,g0)
    c: Equal(g0, g1-g5) x5
    c: PointOnObject(g0,g6)
    c: PointOnObject(g1,g6)
    c: PointOnObject(g2,g6)
    c: PointOnObject(g3,g6)
    c: PointOnObject(g4,g6)
    c: PointOnObject(g5,g6)
    c: Coincident(g6,g-3)
    c: Angle(g4) = 0.785398
    c: Distance(g1,g3) = 5.8
    c: Coincident(g8,g7)
    c: Coincident(g9,g8)
    c: Coincident(g9,g0)
    c: Tangent(g7,g4) = -1.5708
    c: Tangent(g9,g1)
    c: Perpendicular(g8,g7)
    c: Distance(g7) = 2
FEATURE [PartDesign::Pocket] Pocket476  label="Nuthole #005"
  BaseFeature = -> Pocket473
  Length = 3
  Length2 = 100
  Profile = -> Sketch1342
  Type = 0
FEATURE [PartDesign::Pocket] Pocket488  label="Nuthole #006"
  BaseFeature = -> Pocket476
  Length = 3
  Length2 = 100
  Profile = -> Sketch1357
  Reversed = true
  Type = 0
FEATURE [PartDesign::Chamfer] Chamfer242  label="Smooth Nutholes002"
  Base = -> Pocket488 [Edge206,Edge207,Edge141,Edge209,Edge208,Edge225,Edge222,Edge223,Edge224,Edge221]
  BaseFeature = -> Pocket488
  Size = 0.625
FEATURE [Sketcher::SketchObject] Sketch1326
  MapMode = 5
  Placement = pos=(0,0,10) rot=(0,0,1;0rad)
  Support = -> [Chamfer242]
  sketch-geometry (4):
    g0: LineSegment StartX=0 StartY=0 StartZ=0 EndX=56.5 EndY=0 EndZ=0
    g1: LineSegment StartX=56.5 StartY=0 StartZ=0 EndX=56.5 EndY=5 EndZ=0
    g2: LineSegment StartX=56.5 StartY=5 StartZ=0 EndX=0 EndY=5 EndZ=0
    g3: LineSegment StartX=0 StartY=5 StartZ=0 EndX=0 EndY=0 EndZ=0
  constraints (11):
    c: Coincident(g0,g1)
    c: Coincident(g1,g2)
    c: Coincident(g2,g3)
    c: Coincident(g3,g0)
    c: Horizontal(g0)
    c: Horizontal(g2)
    c: Vertical(g1)
    c: Vertical(g3)
    c: Coincident(g0,g-1)
    c: DistanceY(g1,g1) = 5
    c: DistanceX(g2,g2) = 56.5
FEATURE [PartDesign::Pocket] Pocket487  label="Shorten Baseplate002"
  BaseFeature = -> Chamfer242
  Length = 10
  Length2 = 100
  Profile = -> Sketch1326
  Type = 0
FEATURE [PartDesign::Fillet] Fillet155  label="Smooth Corners002"
  Base = -> Pocket487 [Edge232,Edge234,Edge240,Edge242,Edge193,Edge83,Edge85,Edge86,Edge88,Edge170,Edge236,Edge238,Edge258]
  BaseFeature = -> Pocket487
  Radius = 0.4
FEATURE [PartDesign::Body] Body351  label="Wrist002"
  Group = -> [Sketch1337,Pad526,Sketch1344,Pocket494,Fillet156,Sketch1171,Pocket471,Pad527,Sketch1351,Pocket478,Sketch1345,Pocket484,Fillet147,Sketch1336,Pocket477,Sketch1350,Pocket473,Sketch1342,Sketch1357,Pocket476,Pocket488,Chamfer242,Sketch1326,Pocket487,Fillet155]
  Origin = -> Origin484
  Placement = pos=(-66.468,-10,83.4386) rot=(0.281085,0.678598,0.678598;3.68962rad)
  Tip = -> Fillet155
FEATURE [PartDesign::Pad] Pad538
  Length = 10
  Length2 = 100
  Placement = pos=(0,0,0) rot=(1,0,0;1.5708rad)
  Profile = -> Sketch1298
  Reversed = true
  Type = 0
FEATURE [PartDesign::Body] Body379  label="orange wire010"
  Group = -> [Sketch1298,Pad538]
  Origin = -> Origin415
  Placement = pos=(0,25.15,0) rot=(0,0,1;0rad)
  Tip = -> Pad538
FEATURE [PartDesign::Pad] Pad539  label="M3 Nut Primitive107"
  Length = 1.2
  Length2 = 1.2
  Profile = -> Sketch1293
  Type = 4
FEATURE [Sketcher::SketchObject] Sketch1346
  ExternalGeometry = -> [Pad539]
  MapMode = 5
  Placement = pos=(0,0,0) rot=(0.57735,0.57735,0.57735;2.0944rad)
  Support = -> [YZ_Plane490]
  sketch-geometry (6):
    g0: LineSegment StartX=-2.67543 StartY=1.2 StartZ=0 EndX=-3.67543 EndY=1.2 EndZ=0
    g1: LineSegment StartX=-3.67543 StartY=1.2 StartZ=0 EndX=-3.67543 EndY=-1.2 EndZ=0
    g2: LineSegment StartX=-3.67543 StartY=-1.2 StartZ=0 EndX=-2.67543 EndY=-1.2 EndZ=0
    g3: LineSegment StartX=-2.67543 StartY=-1.2 StartZ=0 EndX=-3.17543 EndY=-1 EndZ=0
    g4: LineSegment StartX=-3.17543 StartY=-1 StartZ=0 EndX=-3.17543 EndY=1 EndZ=0
    g5: LineSegment StartX=-3.17543 StartY=1 StartZ=0 EndX=-2.67543 EndY=1.2 EndZ=0
  constraints (15):
    c: Horizontal(g0)
    c: Coincident(g0,g1)
    c: Coincident(g1,g2)
    c: Coincident(g2,g3)
    c: Coincident(g3,g4)
    c: Coincident(g4,g5)
    c: Coincident(g5,g0)
    c: Symmetric(g4,g3,g-1)
    c: Symmetric(g0,g2,g-1)
    c: Symmetric(g1,g0,g-1)
    c: DistanceX(g0,g4) = 0.5
    c: DistanceY(g3,g4) = 2
    c: DistanceY(g1,g0) = 2.4
    c: PointOnObject(g3,g-3)
    c: DistanceX(g4,g0) = 0.5
FEATURE [PartDesign::Pad] Pad540  label="M3 Nut Primitive108"
  Length = 1.2
  Length2 = 1.2
  Profile = -> Sketch1367
  Type = 4
FEATURE [Sketcher::SketchObject] Sketch1361
  ExternalGeometry = -> [Pad540]
  MapMode = 5
  Placement = pos=(0,0,0) rot=(0.57735,0.57735,0.57735;2.0944rad)
  Support = -> [YZ_Plane471]
  sketch-geometry (6):
    g0: LineSegment StartX=-2.67543 StartY=1.2 StartZ=0 EndX=-3.67543 EndY=1.2 EndZ=0
    g1: LineSegment StartX=-3.67543 StartY=1.2 StartZ=0 EndX=-3.67543 EndY=-1.2 EndZ=0
    g2: LineSegment StartX=-3.67543 StartY=-1.2 StartZ=0 EndX=-2.67543 EndY=-1.2 EndZ=0
    g3: LineSegment StartX=-2.67543 StartY=-1.2 StartZ=0 EndX=-3.17543 EndY=-1 EndZ=0
    g4: LineSegment StartX=-3.17543 StartY=-1 StartZ=0 EndX=-3.17543 EndY=1 EndZ=0
    g5: LineSegment StartX=-3.17543 StartY=1 StartZ=0 EndX=-2.67543 EndY=1.2 EndZ=0
  constraints (15):
    c: Horizontal(g0)
    c: Coincident(g0,g1)
    c: Coincident(g1,g2)
    c: Coincident(g2,g3)
    c: Coincident(g3,g4)
    c: Coincident(g4,g5)
    c: Coincident(g5,g0)
    c: Symmetric(g4,g3,g-1)
    c: Symmetric(g0,g2,g-1)
    c: Symmetric(g1,g0,g-1)
    c: DistanceX(g0,g4) = 0.5
    c: DistanceY(g3,g4) = 2
    c: DistanceY(g1,g0) = 2.4
    c: PointOnObject(g3,g-3)
    c: DistanceX(g4,g0) = 0.5
FEATURE [PartDesign::Groove] Groove096  label="M3 Nut Smooth092"
  Angle = 360
  Axis = (-2e-16,3e-16,1)
  Base = (0,0,0)
  BaseFeature = -> Pad540
  Profile = -> Sketch1361
  ReferenceAxis = -> Sketch1361 [V_Axis]
  Reversed = true
FEATURE [PartDesign::Chamfer] Chamfer243  label="M3 Nut Smooth Hole102"
  Base = -> Groove096 [Edge24,Edge23]
  BaseFeature = -> Groove096
  Size = 0.2
FEATURE [PartDesign::Body] Body297  label="M3 Nut052"
  Group = -> [Sketch1367,Pad540,Sketch1361,Groove096,Chamfer243]
  Origin = -> Origin507
  Placement = pos=(0.75,5.5,34.25) rot=(1,0,0;1.5708rad)
  Tip = -> Chamfer243
FEATURE [App::Part] Part114  label="Nuts002"
  Group = -> [Body350,Body297]
  Origin = -> Origin471
FEATURE [PartDesign::Pocket] Pocket497  label="Servopocket002"
  BaseFeature = -> Pad532
  Length = 20
  Length2 = 100
  Profile = -> Sketch1288
  Type = 0
FEATURE [Sketcher::SketchObject] Sketch1274
  MapMode = 5
  Placement = pos=(0,0,25) rot=(0,0,1;0rad)
  Support = -> [Pocket497]
  sketch-geometry (5):
    g0: ArcOfCircle CenterX=22.5 CenterY=23.1875 CenterZ=0 NormalX=0 NormalY=0 NormalZ=1 AngleXU=0 Radius=45.1875 StartAngle=4.19118 EndAngle=4.71239
    g1: LineSegment StartX=22.5 StartY=-22 StartZ=0 EndX=56.5 EndY=-22 EndZ=0
    g2: LineSegment StartX=56.5 StartY=-22 StartZ=0 EndX=56.5 EndY=-23 EndZ=0
    g3: LineSegment StartX=56.5 StartY=-23 StartZ=0 EndX=0 EndY=-23 EndZ=0
    g4: LineSegment StartX=0 StartY=-23 StartZ=0 EndX=0 EndY=-16 EndZ=0
  constraints (15):
    c: PointOnObject(g0,g-2)
    c: Horizontal(g1)
    c: Coincident(g2,g1)
    c: Vertical(g2)
    c: Coincident(g3,g2)
    c: Horizontal(g3)
    c: Coincident(g4,g3)
    c: Coincident(g4,g0)
    c: Vertical(g4)
    c: Tangent(g1,g0) = -1.5708
    c: DistanceX(g0,g0) = 22.5
    c: DistanceY(g4,g4) = 7
    c: DistanceY(g2,g2) = 1
    c: DistanceY(g0,g-1) = 16
    c: DistanceX(g3,g3) = 56.5
FEATURE [PartDesign::Pocket] Pocket480  label="Swing Counterpart002"
  BaseFeature = -> Pocket497
  Length = 25
  Length2 = 100
  Profile = -> Sketch1274
  Type = 0
FEATURE [Sketcher::SketchObject] Sketch1280
  MapMode = 5
  Placement = pos=(56.5,0,0) rot=(0.57735,0.57735,0.57735;2.0944rad)
  Support = -> [Pocket480]
  sketch-geometry (8):
    g0: LineSegment StartX=-6 StartY=22.9 StartZ=0 EndX=-3 EndY=22.9 EndZ=0
    g1: LineSegment StartX=-3 StartY=22.9 StartZ=0 EndX=-3 EndY=17.1 EndZ=0
    g2: LineSegment StartX=-3 StartY=17.1 StartZ=0 EndX=-6 EndY=17.1 EndZ=0
    g3: LineSegment StartX=-6 StartY=17.1 StartZ=0 EndX=-6 EndY=22.9 EndZ=0
    g4: LineSegment StartX=-6 StartY=12.9 StartZ=0 EndX=-3 EndY=12.9 EndZ=0
    g5: LineSegment StartX=-3 StartY=12.9 StartZ=0 EndX=-3 EndY=7.1 EndZ=0
    g6: LineSegment StartX=-3 StartY=7.1 StartZ=0 EndX=-6 EndY=7.1 EndZ=0
    g7: LineSegment StartX=-6 StartY=7.1 StartZ=0 EndX=-6 EndY=12.9 EndZ=0
  constraints (24):
    c: Coincident(g0,g1)
    c: Coincident(g1,g2)
    c: Coincident(g2,g3)
    c: Coincident(g3,g0)
    c: Horizontal(g0)
    c: Horizontal(g2)
    c: Vertical(g1)
    c: Vertical(g3)
    c: Coincident(g4,g5)
    c: Coincident(g5,g6)
    c: Coincident(g6,g7)
    c: Coincident(g7,g4)
    c: Horizontal(g4)
    c: Horizontal(g6)
    c: Vertical(g5)
    c: Vertical(g7)
    c: Equal(g1,g5)
    c: Equal(g4,g2)
    c: Vertical(g1,g4)
    c: DistanceX(g0,g0) = 3
    c: DistanceY(g1,g1) = 5.8
    c: DistanceY(g5,g1) = 10
    c: DistanceY(g-1,g5) = 7.1
    c: DistanceX(g5,g-1) = 3
FEATURE [PartDesign::Pocket] Pocket461  label="Nutholes002"
  BaseFeature = -> Pocket480
  Length = 56.5
  Length2 = 100
  Profile = -> Sketch1280
  Type = 0
FEATURE [Sketcher::SketchObject] Sketch1281
  MapMode = 5
  Placement = pos=(0,0,0) rot=(0,0.707107,0.707107;3.14159rad)
  Support = -> [Pocket461]
  sketch-geometry (4):
    g0: Circle CenterX=-52.5 CenterY=20 CenterZ=0 NormalX=0 NormalY=0 NormalZ=1 AngleXU=0 Radius=1.6
    g1: Circle CenterX=-52.5 CenterY=10 CenterZ=0 NormalX=0 NormalY=0 NormalZ=1 AngleXU=0 Radius=1.6
    g2: Circle CenterX=-4 CenterY=20 CenterZ=0 NormalX=0 NormalY=0 NormalZ=1 AngleXU=0 Radius=1.6
    g3: Circle CenterX=-4 CenterY=10 CenterZ=0 NormalX=0 NormalY=0 NormalZ=1 AngleXU=0 Radius=1.6
  constraints (12):
    c: Horizontal(g2,g0)
    c: Horizontal(g1,g3)
    c: Vertical(g3,g2)
    c: Vertical(g0,g1)
    c: Equal(g0,g1)
    c: Equal(g1,g2)
    c: Equal(g2,g3)
    c: Radius(g2) = 1.6
    c: DistanceX(g0,g2) = 48.5
    c: DistanceY(g3,g2) = 10
    c: DistanceY(g-1,g3) = 10
    c: DistanceX(g3,g-1) = 4
FEATURE [PartDesign::Pad] Pad542  label="Baseblock012"
  Length = 26.6
  Length2 = 100
  Profile = -> Sketch1348
  Type = 0
FEATURE [Sketcher::SketchObject] Sketch1299
  MapMode = 5
  Placement = pos=(0,0,26.6) rot=(0,0,1;0rad)
  Support = -> [Pad542]
  sketch-geometry (4):
    g0: LineSegment StartX=-10 StartY=-26.8 StartZ=0 EndX=10 EndY=-26.8 EndZ=0
    g1: LineSegment StartX=10 StartY=-26.8 StartZ=0 EndX=10 EndY=26.8 EndZ=0
    g2: LineSegment StartX=10 StartY=26.8 StartZ=0 EndX=-10 EndY=26.8 EndZ=0
    g3: LineSegment StartX=-10 StartY=26.8 StartZ=0 EndX=-10 EndY=-26.8 EndZ=0
  constraints (10):
    c: Coincident(g0,g1)
    c: Coincident(g1,g2)
    c: Coincident(g2,g3)
    c: Coincident(g3,g0)
    c: Horizontal(g0)
    c: Vertical(g3)
    c: Symmetric(g1,g2,g-2)
    c: Symmetric(g1,g0,g-1)
    c: DistanceX(g2,g2) = 20
    c: DistanceY(g1,g1) = 53.6
FEATURE [PartDesign::Pad] Pad488
  BaseFeature = -> Pad542
  Length = 2.5
  Length2 = 100
  Profile = -> Sketch1299
  Type = 0
FEATURE [Sketcher::SketchObject] Sketch1319
  MapMode = 5
  Placement = pos=(0,0,29.1) rot=(0,0,1;0rad)
  Support = -> [Pad488]
  sketch-geometry (4):
    g0: LineSegment StartX=-10 StartY=-20.15 StartZ=0 EndX=10 EndY=-20.15 EndZ=0
    g1: LineSegment StartX=10 StartY=-20.15 StartZ=0 EndX=10 EndY=20.15 EndZ=0
    g2: LineSegment StartX=10 StartY=20.15 StartZ=0 EndX=-10 EndY=20.15 EndZ=0
    g3: LineSegment StartX=-10 StartY=20.15 StartZ=0 EndX=-10 EndY=-20.15 EndZ=0
  constraints (10):
    c: Coincident(g0,g1)
    c: Coincident(g1,g2)
    c: Coincident(g2,g3)
    c: Coincident(g3,g0)
    c: Horizontal(g0)
    c: Vertical(g3)
    c: Symmetric(g1,g2,g-2)
    c: Symmetric(g1,g0,g-1)
    c: DistanceX(g2,g2) = 20
    c: DistanceY(g1,g1) = 40.3
FEATURE [PartDesign::Pad] Pad487
  BaseFeature = -> Pad488
  Length = 6
  Length2 = 100
  Profile = -> Sketch1319
  Type = 0
FEATURE [Sketcher::SketchObject] Sketch1323
  ExternalGeometry = -> [Pad487]
  MapMode = 5
  Placement = pos=(0,0,35.1) rot=(0,0,1;0rad)
  Support = -> [Pad487]
  sketch-geometry (7):
    g0: ArcOfCircle CenterX=-3e-16 CenterY=10.15 CenterZ=0 NormalX=0 NormalY=0 NormalZ=1 AngleXU=0 Radius=9.5 StartAngle=5.9573 EndAngle=9.75066
    g1: LineSegment StartX=-9 StartY=7.10862 StartZ=0 EndX=-9 EndY=-14.15 EndZ=0
    g2: LineSegment StartX=-9 StartY=-14.15 StartZ=0 EndX=-5 EndY=-14.15 EndZ=0
    g3: LineSegment StartX=5 StartY=-14.15 StartZ=0 EndX=9 EndY=-14.15 EndZ=0
    g4: LineSegment StartX=9 StartY=-14.15 StartZ=0 EndX=9 EndY=7.10862 EndZ=0
    g5: ArcOfCircle CenterX=-3e-16 CenterY=-10.4 CenterZ=0 NormalX=0 NormalY=0 NormalZ=1 AngleXU=0 Radius=6.25 StartAngle=3.78509 EndAngle=5.63968
    g6: LineSegment [constr] StartX=0 StartY=-20.15 StartZ=0 EndX=0 EndY=-16.65 EndZ=0
  constraints (22):
    c: Symmetric(g0,g0,g-2)
    c: Coincident(g1,g0)
    c: Vertical(g1)
    c: Coincident(g2,g1)
    c: Horizontal(g2)
    c: Horizontal(g3)
    c: Coincident(g4,g3)
    c: Coincident(g4,g0)
    c: Vertical(g4)
    c: Symmetric(g2,g3,g-2)
    c: Coincident(g5,g2)
    c: Coincident(g5,g3)
    c: DistanceY(g-3,g3) = 6
    c: DistanceY(g0,g-4) = 10
    c: Radius(g0) = 9.5
    c: DistanceX(g0,g0) = 18
    c: PointOnObject(g6,g-3)
    c: PointOnObject(g6,g5)
    c: Vertical(g6)
    c: DistanceY(g6,g6) = 3.5
    c: DistanceX(g2,g3) = 10
    c: PointOnObject(g6,g-2)
FEATURE [PartDesign::Pad] Pad486
  BaseFeature = -> Pad487
  Length = 2.5
  Length2 = 100
  Profile = -> Sketch1323
  Type = 0
FEATURE [Sketcher::SketchObject] Sketch1304
  ExternalGeometry = -> [Pad486]
  MapMode = 5
  Placement = pos=(0,0,37.6) rot=(0,0,1;0rad)
  Support = -> [Pad486]
  sketch-geometry (1):
    g0: Circle CenterX=-3e-16 CenterY=10.15 CenterZ=0 NormalX=0 NormalY=0 NormalZ=1 AngleXU=0 Radius=6.5
  constraints (2):
    c: Coincident(g0,g-3)
    c: Radius(g0) = 6.5
FEATURE [PartDesign::Pad] Pad544  label="M3x8 Head065"
  Length = 3
  Length2 = 100
  Profile = -> Sketch1276
  Type = 0
FEATURE [Sketcher::SketchObject] Sketch1362
  MapMode = 5
  Placement = pos=(0,0,3) rot=(0,0,1;0rad)
  Support = -> [Pad544]
  sketch-geometry (1):
    g0: Circle CenterX=0 CenterY=0 CenterZ=0 NormalX=0 NormalY=0 NormalZ=1 AngleXU=0 Radius=1.5
  constraints (2):
    c: Coincident(g0,g-1)
    c: Radius(g0) = 1.5
FEATURE [PartDesign::Pad] Pad541  label="M3x8 Thread064"
  BaseFeature = -> Pad544
  Length = 8
  Length2 = 100
  Profile = -> Sketch1362
  Type = 0
FEATURE [Sketcher::SketchObject] Sketch1356
  MapMode = 5
  Placement = pos=(0,0,0) rot=(1,0,0;3.14159rad)
  Support = -> [Pad541]
  sketch-geometry (7):
    g0: LineSegment StartX=1.275 StartY=0.736122 StartZ=0 EndX=0 EndY=1.47224 EndZ=0
    g1: LineSegment StartX=0 StartY=1.47224 StartZ=0 EndX=-1.275 EndY=0.736122 EndZ=0
    g2: LineSegment StartX=-1.275 StartY=0.736122 StartZ=0 EndX=-1.275 EndY=-0.736122 EndZ=0
    g3: LineSegment StartX=-1.275 StartY=-0.736122 StartZ=0 EndX=1.34766e-11 EndY=-1.47224 EndZ=0
    g4: LineSegment StartX=1.34766e-11 StartY=-1.47224 StartZ=0 EndX=1.275 EndY=-0.736122 EndZ=0
    g5: LineSegment StartX=1.275 StartY=-0.736122 StartZ=0 EndX=1.275 EndY=0.736122 EndZ=0
    g6: Circle [constr] CenterX=0 CenterY=0 CenterZ=0 NormalX=0 NormalY=0 NormalZ=1 AngleXU=0 Radius=1.47224
  constraints (16):
    c: Coincident(g0,g1)
    c: Coincident(g1,g2)
    c: Coincident(g2,g3)
    c: Coincident(g3,g4)
    c: Coincident(g4,g5)
    c: Coincident(g5,g0)
    c: Equal(g0, g1-g5) x5
    c: PointOnObject(g0,g6)
    c: PointOnObject(g1,g6)
    c: PointOnObject(g2,g6)
    c: PointOnObject(g3,g6)
    c: PointOnObject(g4,g6)
    c: PointOnObject(g5,g6)
    c: Coincident(g6,g-1)
    c: PointOnObject(g0,g-2)
    c: DistanceX(g1,g0) = 2.55
FEATURE [PartDesign::Pocket] Pocket498  label="M3x8 Wrench064"
  BaseFeature = -> Pad541
  Length = 1.3
  Length2 = 100
  Profile = -> Sketch1356
  Type = 0
FEATURE [PartDesign::Chamfer] Chamfer224  label="M3x8 Smooth059"
  Base = -> Pocket498 [Face11,Edge2,Edge24,Edge3]
  BaseFeature = -> Pocket498
  Size = 0.2
FEATURE [PartDesign::Body] Body317  label="M3x066"
  Group = -> [Sketch1276,Pad544,Sketch1362,Pad541,Sketch1356,Pocket498,Chamfer224]
  Origin = -> Origin426
  Placement = pos=(0.75,-14,34.25) rot=(-1,0,0;1.5708rad)
  Tip = -> Chamfer224
FEATURE [PartDesign::Pocket] Pocket501  label="Screwholes004"
  BaseFeature = -> Pocket461
  Length = 8.5
  Length2 = 100
  Profile = -> Sketch1281
  Type = 0
FEATURE [Sketcher::SketchObject] Sketch1369
  MapMode = 5
  Placement = pos=(56.5,0,0) rot=(0.57735,0.57735,0.57735;2.0944rad)
  Support = -> [Pocket501]
  sketch-geometry (4):
    g0: ArcOfCircle CenterX=-12 CenterY=11.5 CenterZ=0 NormalX=0 NormalY=0 NormalZ=1 AngleXU=0 Radius=2.5 StartAngle=3.14159 EndAngle=6.28319
    g1: LineSegment StartX=-14.5 StartY=11.5 StartZ=0 EndX=-14.5 EndY=25 EndZ=0
    g2: LineSegment StartX=-14.5 StartY=25 StartZ=0 EndX=-9.5 EndY=25 EndZ=0
    g3: LineSegment StartX=-9.5 StartY=25 StartZ=0 EndX=-9.5 EndY=11.5 EndZ=0
  constraints (13):
    c: Horizontal(g0,g0)
    c: Horizontal(g0,g0)
    c: Coincident(g1,g0)
    c: Vertical(g1)
    c: Coincident(g2,g1)
    c: Horizontal(g2)
    c: Coincident(g3,g2)
    c: Coincident(g3,g0)
    c: Vertical(g3)
    c: Radius(g0) = 2.5
    c: DistanceX(g0,g-1) = 12
    c: DistanceY(g-1,g0) = 11.5
    c: DistanceY(g-1,g2) = 25
FEATURE [PartDesign::Pocket] Pocket485  label="Servocable Pocket002"
  BaseFeature = -> Pocket501
  Length = 8
  Length2 = 100
  Profile = -> Sketch1369
  Type = 0
FEATURE [PartDesign::Pad] Pad545  label="M3x8 Thread065"
  BaseFeature = -> Pad530
  Length = 8
  Length2 = 100
  Profile = -> Sketch1355
  Type = 0
FEATURE [Sketcher::SketchObject] Sketch1360
  MapMode = 5
  Placement = pos=(0,0,0) rot=(1,0,0;3.14159rad)
  Support = -> [Pad545]
  sketch-geometry (7):
    g0: LineSegment StartX=1.275 StartY=0.736122 StartZ=0 EndX=0 EndY=1.47224 EndZ=0
    g1: LineSegment StartX=0 StartY=1.47224 StartZ=0 EndX=-1.275 EndY=0.736122 EndZ=0
    g2: LineSegment StartX=-1.275 StartY=0.736122 StartZ=0 EndX=-1.275 EndY=-0.736122 EndZ=0
    g3: LineSegment StartX=-1.275 StartY=-0.736122 StartZ=0 EndX=1.34766e-11 EndY=-1.47224 EndZ=0
    g4: LineSegment StartX=1.34766e-11 StartY=-1.47224 StartZ=0 EndX=1.275 EndY=-0.736122 EndZ=0
    g5: LineSegment StartX=1.275 StartY=-0.736122 StartZ=0 EndX=1.275 EndY=0.736122 EndZ=0
    g6: Circle [constr] CenterX=0 CenterY=0 CenterZ=0 NormalX=0 NormalY=0 NormalZ=1 AngleXU=0 Radius=1.47224
  constraints (16):
    c: Coincident(g0,g1)
    c: Coincident(g1,g2)
    c: Coincident(g2,g3)
    c: Coincident(g3,g4)
    c: Coincident(g4,g5)
    c: Coincident(g5,g0)
    c: Equal(g0, g1-g5) x5
    c: PointOnObject(g0,g6)
    c: PointOnObject(g1,g6)
    c: PointOnObject(g2,g6)
    c: PointOnObject(g3,g6)
    c: PointOnObject(g4,g6)
    c: PointOnObject(g5,g6)
    c: Coincident(g6,g-1)
    c: PointOnObject(g0,g-2)
    c: DistanceX(g1,g0) = 2.55
FEATURE [PartDesign::Groove] Groove113  label="M3 Nut Smooth107"
  Angle = 360
  Axis = (-2e-16,3e-16,1)
  Base = (0,0,0)
  BaseFeature = -> Pad539
  Profile = -> Sketch1346
  ReferenceAxis = -> Sketch1346 [V_Axis]
  Reversed = true
FEATURE [PartDesign::Revolution] Revolution024
  Angle = 360
  Axis = (0,2e-16,1)
  Base = (0,0,0)
  Placement = pos=(0,0,0) rot=(1,0,0;1.5708rad)
  Profile = -> Sketch1236
  ReferenceAxis = -> Sketch1236 [V_Axis]
FEATURE [PartDesign::Fillet] Fillet166
  Base = -> Revolution024 [Face2,Face6,Edge1,Edge11,Face4]
  BaseFeature = -> Revolution024
  Placement = pos=(0,0,0) rot=(1,0,0;1.5708rad)
  Radius = 0.25
FEATURE [PartDesign::Body] Body390  label="Rubber Dampener030"
  Group = -> [Sketch1236,Revolution024,Fillet166]
  Origin = -> Origin461
  Placement = pos=(-62.3,-12.25,93.7) rot=(-1,0,0;1.5708rad)
  Tip = -> Fillet166
FEATURE [PartDesign::Pocket] Pocket502
  BaseFeature = -> Pad476
  Length = 4
  Length2 = 100
  Profile = -> Sketch1314
  Type = 0
FEATURE [PartDesign::Chamfer] Chamfer217
  Base = -> Pocket502 [Edge3]
  BaseFeature = -> Pocket502
  Size = 0.25
FEATURE [PartDesign::Body] Body304  label="Gear009"
  Group = -> [Sketch1322,Pad476,Sketch1314,Pocket502,Chamfer217]
  Origin = -> Origin472
  Placement = pos=(0,0,38.25) rot=(0,0,1;0rad)
  Tip = -> Chamfer217
FEATURE [PartDesign::Pad] Pad547  label="Baseblock013"
  Length = 26.6
  Length2 = 100
  Profile = -> Sketch1196
  Type = 0
FEATURE [Sketcher::SketchObject] Sketch1208
  MapMode = 5
  Placement = pos=(0,0,26.6) rot=(0,0,1;0rad)
  Support = -> [Pad547]
  sketch-geometry (4):
    g0: LineSegment StartX=-10 StartY=-26.8 StartZ=0 EndX=10 EndY=-26.8 EndZ=0
    g1: LineSegment StartX=10 StartY=-26.8 StartZ=0 EndX=10 EndY=26.8 EndZ=0
    g2: LineSegment StartX=10 StartY=26.8 StartZ=0 EndX=-10 EndY=26.8 EndZ=0
    g3: LineSegment StartX=-10 StartY=26.8 StartZ=0 EndX=-10 EndY=-26.8 EndZ=0
  constraints (10):
    c: Coincident(g0,g1)
    c: Coincident(g1,g2)
    c: Coincident(g2,g3)
    c: Coincident(g3,g0)
    c: Horizontal(g0)
    c: Vertical(g3)
    c: Symmetric(g1,g2,g-2)
    c: Symmetric(g1,g0,g-1)
    c: DistanceX(g2,g2) = 20
    c: DistanceY(g1,g1) = 53.6
FEATURE [PartDesign::Pad] Pad549
  Length = 10
  Length2 = 100
  Placement = pos=(0,0,0) rot=(1,0,0;1.5708rad)
  Profile = -> Sketch1226
  Reversed = true
  Type = 0
FEATURE [PartDesign::Pad] Pad550  label="M3x20 Thread042"
  BaseFeature = -> Pad534
  Length = 20
  Length2 = 100
  Profile = -> Sketch1334
  Type = 0
FEATURE [Sketcher::SketchObject] Sketch1339
  MapMode = 5
  Placement = pos=(0,0,0) rot=(1,0,0;3.14159rad)
  Support = -> [Pad550]
  sketch-geometry (7):
    g0: LineSegment StartX=1.275 StartY=0.736122 StartZ=0 EndX=0 EndY=1.47224 EndZ=0
    g1: LineSegment StartX=0 StartY=1.47224 StartZ=0 EndX=-1.275 EndY=0.736122 EndZ=0
    g2: LineSegment StartX=-1.275 StartY=0.736122 StartZ=0 EndX=-1.275 EndY=-0.736122 EndZ=0
    g3: LineSegment StartX=-1.275 StartY=-0.736122 StartZ=0 EndX=1.34766e-11 EndY=-1.47224 EndZ=0
    g4: LineSegment StartX=1.34766e-11 StartY=-1.47224 StartZ=0 EndX=1.275 EndY=-0.736122 EndZ=0
    g5: LineSegment StartX=1.275 StartY=-0.736122 StartZ=0 EndX=1.275 EndY=0.736122 EndZ=0
    g6: Circle [constr] CenterX=0 CenterY=0 CenterZ=0 NormalX=0 NormalY=0 NormalZ=1 AngleXU=0 Radius=1.47224
  constraints (16):
    c: Coincident(g0,g1)
    c: Coincident(g1,g2)
    c: Coincident(g2,g3)
    c: Coincident(g3,g4)
    c: Coincident(g4,g5)
    c: Coincident(g5,g0)
    c: Equal(g0, g1-g5) x5
    c: PointOnObject(g0,g6)
    c: PointOnObject(g1,g6)
    c: PointOnObject(g2,g6)
    c: PointOnObject(g3,g6)
    c: PointOnObject(g4,g6)
    c: PointOnObject(g5,g6)
    c: Coincident(g6,g-1)
    c: PointOnObject(g0,g-2)
    c: DistanceX(g1,g0) = 2.55
FEATURE [PartDesign::Pocket] Pocket504  label="M3x8 Wrench065"
  BaseFeature = -> Pad545
  Length = 1.3
  Length2 = 100
  Profile = -> Sketch1360
  Type = 0
FEATURE [PartDesign::Chamfer] Chamfer220  label="M3x8 Smooth057"
  Base = -> Pocket504 [Face11,Edge2,Edge24,Edge3]
  BaseFeature = -> Pocket504
  Size = 0.2
FEATURE [PartDesign::Body] Body339  label="M3x070"
  Group = -> [Sketch1366,Pad530,Sketch1355,Pad545,Sketch1360,Pocket504,Chamfer220]
  Origin = -> Origin482
  Placement = pos=(0.72,13.88,34.3) rot=(1,0,0;1.5708rad)
  Tip = -> Chamfer220
FEATURE [App::Part] Part125  label="Screws008"
  Group = -> [Body317,Body339]
  Origin = -> Origin434
FEATURE [PartDesign::Pad] Pad553  label="M3x20 Head043"
  Length = 3
  Length2 = 100
  Profile = -> Sketch1220
  Type = 0
FEATURE [PartDesign::Pad] Pad555  label="M3 Nut Primitive109"
  Length = 1.2
  Length2 = 1.2
  Profile = -> Sketch1214
  Type = 4
FEATURE [Sketcher::SketchObject] Sketch1217
  ExternalGeometry = -> [Pad555]
  MapMode = 5
  Placement = pos=(0,0,0) rot=(0.57735,0.57735,0.57735;2.0944rad)
  Support = -> [YZ_Plane426]
  sketch-geometry (6):
    g0: LineSegment StartX=-2.67543 StartY=1.2 StartZ=0 EndX=-3.67543 EndY=1.2 EndZ=0
    g1: LineSegment StartX=-3.67543 StartY=1.2 StartZ=0 EndX=-3.67543 EndY=-1.2 EndZ=0
    g2: LineSegment StartX=-3.67543 StartY=-1.2 StartZ=0 EndX=-2.67543 EndY=-1.2 EndZ=0
    g3: LineSegment StartX=-2.67543 StartY=-1.2 StartZ=0 EndX=-3.17543 EndY=-1 EndZ=0
    g4: LineSegment StartX=-3.17543 StartY=-1 StartZ=0 EndX=-3.17543 EndY=1 EndZ=0
    g5: LineSegment StartX=-3.17543 StartY=1 StartZ=0 EndX=-2.67543 EndY=1.2 EndZ=0
  constraints (15):
    c: Horizontal(g0)
    c: Coincident(g0,g1)
    c: Coincident(g1,g2)
    c: Coincident(g2,g3)
    c: Coincident(g3,g4)
    c: Coincident(g4,g5)
    c: Coincident(g5,g0)
    c: Symmetric(g4,g3,g-1)
    c: Symmetric(g0,g2,g-1)
    c: Symmetric(g1,g0,g-1)
    c: DistanceX(g0,g4) = 0.5
    c: DistanceY(g3,g4) = 2
    c: DistanceY(g1,g0) = 2.4
    c: PointOnObject(g3,g-3)
    c: DistanceX(g4,g0) = 0.5
FEATURE [PartDesign::Pad] Pad556  label="M3x20 Head044"
  Length = 3
  Length2 = 100
  Profile = -> Sketch1321
  Type = 0
FEATURE [Sketcher::SketchObject] Sketch1297
  MapMode = 5
  Placement = pos=(0,0,3) rot=(0,0,1;0rad)
  Support = -> [Pad556]
  sketch-geometry (1):
    g0: Circle CenterX=0 CenterY=0 CenterZ=0 NormalX=0 NormalY=0 NormalZ=1 AngleXU=0 Radius=1.5
  constraints (2):
    c: Coincident(g0,g-1)
    c: Radius(g0) = 1.5
FEATURE [PartDesign::Pad] Pad537  label="M3x20 Thread041"
  BaseFeature = -> Pad556
  Length = 20
  Length2 = 100
  Profile = -> Sketch1297
  Type = 0
FEATURE [Sketcher::SketchObject] Sketch1320
  MapMode = 5
  Placement = pos=(0,0,0) rot=(1,0,0;3.14159rad)
  Support = -> [Pad537]
  sketch-geometry (7):
    g0: LineSegment StartX=1.275 StartY=0.736122 StartZ=0 EndX=0 EndY=1.47224 EndZ=0
    g1: LineSegment StartX=0 StartY=1.47224 StartZ=0 EndX=-1.275 EndY=0.736122 EndZ=0
    g2: LineSegment StartX=-1.275 StartY=0.736122 StartZ=0 EndX=-1.275 EndY=-0.736122 EndZ=0
    g3: LineSegment StartX=-1.275 StartY=-0.736122 StartZ=0 EndX=1.34766e-11 EndY=-1.47224 EndZ=0
    g4: LineSegment StartX=1.34766e-11 StartY=-1.47224 StartZ=0 EndX=1.275 EndY=-0.736122 EndZ=0
    g5: LineSegment StartX=1.275 StartY=-0.736122 StartZ=0 EndX=1.275 EndY=0.736122 EndZ=0
    g6: Circle [constr] CenterX=0 CenterY=0 CenterZ=0 NormalX=0 NormalY=0 NormalZ=1 AngleXU=0 Radius=1.47224
  constraints (16):
    c: Coincident(g0,g1)
    c: Coincident(g1,g2)
    c: Coincident(g2,g3)
    c: Coincident(g3,g4)
    c: Coincident(g4,g5)
    c: Coincident(g5,g0)
    c: Equal(g0, g1-g5) x5
    c: PointOnObject(g0,g6)
    c: PointOnObject(g1,g6)
    c: PointOnObject(g2,g6)
    c: PointOnObject(g3,g6)
    c: PointOnObject(g4,g6)
    c: PointOnObject(g5,g6)
    c: Coincident(g6,g-1)
    c: PointOnObject(g0,g-2)
    c: DistanceX(g1,g0) = 2.55
FEATURE [PartDesign::Pocket] Pocket500  label="M3x20 Wrench042"
  BaseFeature = -> Pad537
  Length = 1.3
  Length2 = 100
  Profile = -> Sketch1320
  Type = 0
FEATURE [PartDesign::Pad] Pad557  label="M3 Nut Primitive110"
  Length = 1.2
  Length2 = 1.2
  Profile = -> Sketch1317
  Type = 4
FEATURE [Sketcher::SketchObject] Sketch1347
  ExternalGeometry = -> [Pad557]
  MapMode = 5
  Placement = pos=(0,0,0) rot=(0.57735,0.57735,0.57735;2.0944rad)
  Support = -> [YZ_Plane477]
  sketch-geometry (6):
    g0: LineSegment StartX=-2.67543 StartY=1.2 StartZ=0 EndX=-3.67543 EndY=1.2 EndZ=0
    g1: LineSegment StartX=-3.67543 StartY=1.2 StartZ=0 EndX=-3.67543 EndY=-1.2 EndZ=0
    g2: LineSegment StartX=-3.67543 StartY=-1.2 StartZ=0 EndX=-2.67543 EndY=-1.2 EndZ=0
    g3: LineSegment StartX=-2.67543 StartY=-1.2 StartZ=0 EndX=-3.17543 EndY=-1 EndZ=0
    g4: LineSegment StartX=-3.17543 StartY=-1 StartZ=0 EndX=-3.17543 EndY=1 EndZ=0
    g5: LineSegment StartX=-3.17543 StartY=1 StartZ=0 EndX=-2.67543 EndY=1.2 EndZ=0
  constraints (15):
    c: Horizontal(g0)
    c: Coincident(g0,g1)
    c: Coincident(g1,g2)
    c: Coincident(g2,g3)
    c: Coincident(g3,g4)
    c: Coincident(g4,g5)
    c: Coincident(g5,g0)
    c: Symmetric(g4,g3,g-1)
    c: Symmetric(g0,g2,g-1)
    c: Symmetric(g1,g0,g-1)
    c: DistanceX(g0,g4) = 0.5
    c: DistanceY(g3,g4) = 2
    c: DistanceY(g1,g0) = 2.4
    c: PointOnObject(g3,g-3)
    c: DistanceX(g4,g0) = 0.5
FEATURE [PartDesign::Groove] Groove110  label="M3 Nut Smooth104"
  Angle = 360
  Axis = (-2e-16,3e-16,1)
  Base = (0,0,0)
  BaseFeature = -> Pad557
  Profile = -> Sketch1347
  ReferenceAxis = -> Sketch1347 [V_Axis]
  Reversed = true
FEATURE [PartDesign::Pad] Pad558
  BaseFeature = -> Pad486
  Length = 1
  Length2 = 100
  Profile = -> Sketch1304
  Type = 0
FEATURE [Sketcher::SketchObject] Sketch1160
  ExternalGeometry = -> [Pad558]
  MapMode = 5
  Placement = pos=(0,0,38.6) rot=(0,0,1;0rad)
  Support = -> [Pad558]
  sketch-geometry (1):
    g0: Circle CenterX=0 CenterY=10.15 CenterZ=0 NormalX=0 NormalY=0 NormalZ=1 AngleXU=0 Radius=5.5
  constraints (2):
    c: Coincident(g0,g-3)
    c: Radius(g0) = 5.5
FEATURE [PartDesign::Pad] Pad475
  BaseFeature = -> Pad558
  Length = 0.5
  Length2 = 100
  Profile = -> Sketch1160
  Type = 0
FEATURE [Sketcher::SketchObject] Sketch1316
  ExternalGeometry = -> [Pad475]
  MapMode = 5
  Placement = pos=(0,0,39.1) rot=(0,0,1;0rad)
  Support = -> [Pad475]
  sketch-geometry (1):
    g0: Circle CenterX=0 CenterY=10.15 CenterZ=0 NormalX=0 NormalY=0 NormalZ=1 AngleXU=0 Radius=3
  constraints (2):
    c: Coincident(g0,g-3)
    c: Radius(g0) = 3
FEATURE [PartDesign::Pad] Pad554
  BaseFeature = -> Pad475
  Length = 4
  Length2 = 100
  Profile = -> Sketch1316
  Type = 0
FEATURE [Sketcher::SketchObject] Sketch1343
  ExternalGeometry = -> [Pad554]
  MapMode = 5
  Placement = pos=(0,0,43.1) rot=(0,0,1;0rad)
  Support = -> [Pad554]
  sketch-geometry (1):
    g0: Circle CenterX=0 CenterY=10.15 CenterZ=0 NormalX=0 NormalY=0 NormalZ=1 AngleXU=0 Radius=1.5
  constraints (2):
    c: Coincident(g0,g-3)
    c: Radius(g0) = 1.5
FEATURE [PartDesign::Pocket] Pocket425
  BaseFeature = -> Pad554
  Length = 5
  Length2 = 100
  Profile = -> Sketch1343
  Type = 0
FEATURE [Sketcher::SketchObject] Sketch1301
  MapMode = 5
  Placement = pos=(0,0,29.1) rot=(0,0,1;0rad)
  Support = -> [Pocket425]
  sketch-geometry (4):
    g0: Circle CenterX=-4.91157 CenterY=25.3 CenterZ=0 NormalX=0 NormalY=0 NormalZ=1 AngleXU=0 Radius=2.25
    g1: Circle CenterX=4.91157 CenterY=25.3 CenterZ=0 NormalX=0 NormalY=0 NormalZ=1 AngleXU=0 Radius=2.25
    g2: Circle CenterX=-4.91157 CenterY=-25.3 CenterZ=0 NormalX=0 NormalY=0 NormalZ=1 AngleXU=0 Radius=2.25
    g3: Circle CenterX=4.91157 CenterY=-25.3 CenterZ=0 NormalX=0 NormalY=0 NormalZ=1 AngleXU=0 Radius=2.25
  constraints (8):
    c: Equal(g3,g2)
    c: Equal(g2,g1)
    c: Equal(g1,g0)
    c: Radius(g1) = 2.25
    c: Symmetric(g1,g0,g-2)
    c: Symmetric(g3,g2,g-2)
    c: Symmetric(g3,g1,g-1)
    c: DistanceY(g3,g1) = 50.6
FEATURE [PartDesign::Pocket] Pocket505
  BaseFeature = -> Pocket425
  Length = 5
  Length2 = 100
  Profile = -> Sketch1301
  Type = 0
FEATURE [Sketcher::SketchObject] Sketch1313
  MapMode = 5
  Placement = pos=(0,0,29.1) rot=(0,0,1;0rad)
  Support = -> [Pocket505]
  sketch-geometry (8):
    g0: LineSegment StartX=-0.5 StartY=26.8 StartZ=0 EndX=0.5 EndY=26.8 EndZ=0
    g1: LineSegment StartX=0.5 StartY=26.8 StartZ=0 EndX=0.5 EndY=20.15 EndZ=0
    g2: LineSegment StartX=0.5 StartY=20.15 StartZ=0 EndX=-0.5 EndY=20.15 EndZ=0
    g3: LineSegment StartX=-0.5 StartY=20.15 StartZ=0 EndX=-0.5 EndY=26.8 EndZ=0
    g4: LineSegment StartX=-0.5 StartY=-20.15 StartZ=0 EndX=0.5 EndY=-20.15 EndZ=0
    g5: LineSegment StartX=0.5 StartY=-20.15 StartZ=0 EndX=0.5 EndY=-26.8 EndZ=0
    g6: LineSegment StartX=0.5 StartY=-26.8 StartZ=0 EndX=-0.5 EndY=-26.8 EndZ=0
    g7: LineSegment StartX=-0.5 StartY=-26.8 StartZ=0 EndX=-0.5 EndY=-20.15 EndZ=0
  constraints (20):
    c: Coincident(g0,g1)
    c: Coincident(g1,g2)
    c: Coincident(g2,g3)
    c: Coincident(g3,g0)
    c: Horizontal(g2)
    c: Vertical(g1)
    c: Vertical(g3)
    c: Coincident(g4,g5)
    c: Coincident(g5,g6)
    c: Coincident(g6,g7)
    c: Coincident(g7,g4)
    c: Horizontal(g6)
    c: Vertical(g7)
    c: Symmetric(g4,g4,g-2)
    c: Symmetric(g0,g0,g-2)
    c: Symmetric(g0,g5,g-1)
    c: DistanceY(g5,g0) = 53.6
    c: DistanceY(g4,g1) = 40.3
    c: DistanceX(g0,g0) = 1
    c: Symmetric(g4,g1,g-1)
FEATURE [PartDesign::Pad] Pad482
  BaseFeature = -> Pocket505
  Length = 2
  Length2 = 100
  Profile = -> Sketch1313
  Type = 0
FEATURE [Sketcher::SketchObject] Sketch1340
  ExternalGeometry = -> [Pad482]
  MapMode = 5
  Placement = pos=(0.5,0,0) rot=(0.57735,0.57735,0.57735;2.0944rad)
  Support = -> [Pad482]
  sketch-geometry (6):
    g0: LineSegment StartX=-26.8 StartY=29.1 StartZ=0 EndX=-26.8 EndY=31.1 EndZ=0
    g1: LineSegment StartX=-26.8 StartY=31.1 StartZ=0 EndX=-20.15 EndY=31.1 EndZ=0
    g2: LineSegment StartX=-20.15 StartY=31.1 StartZ=0 EndX=-26.8 EndY=29.1 EndZ=0
    g3: LineSegment StartX=20.15 StartY=31.1 StartZ=0 EndX=26.8 EndY=31.1 EndZ=0
    g4: LineSegment StartX=26.8 StartY=31.1 StartZ=0 EndX=26.8 EndY=29.1 EndZ=0
    g5: LineSegment StartX=26.8 StartY=29.1 StartZ=0 EndX=20.15 EndY=31.1 EndZ=0
  constraints (14):
    c: Vertical(g0)
    c: Coincident(g0,g1)
    c: Horizontal(g1)
    c: Coincident(g1,g2)
    c: Coincident(g2,g0)
    c: Coincident(g3,g4)
    c: Coincident(g4,g5)
    c: Coincident(g5,g3)
    c: Symmetric(g0,g4,g-2)
    c: Symmetric(g3,g0,g-2)
    c: Symmetric(g1,g3,g-2)
    c: DistanceX(g0,g3) = 53.6
    c: DistanceY(g4,g4) = 2
    c: Coincident(g3,g-3)
FEATURE [PartDesign::Pocket] Pocket437
  BaseFeature = -> Pad482
  Length = 1
  Length2 = 100
  Profile = -> Sketch1340
  Type = 0
FEATURE [PartDesign::Fillet] Fillet149
  Base = -> Pocket437 [Edge26,Edge27,Edge72,Edge63,Edge70,Edge78,Edge51,Edge49,Edge71,Edge50,Edge79,Edge86,Edge30,Edge21,Edge4,Edge29,Edge105,Edge107,Edge109,Edge111,Edge113,Edge114,Edge123]
  BaseFeature = -> Pocket437
  Radius = 0.4
FEATURE [Sketcher::SketchObject] Sketch1327
  MapMode = 5
  Placement = pos=(0,20.15,0) rot=(0,0.707107,0.707107;3.14159rad)
  Support = -> [Fillet149]
  sketch-geometry (4):
    g0: LineSegment StartX=-3.25 StartY=2 StartZ=0 EndX=3.25 EndY=2 EndZ=0
    g1: LineSegment StartX=3.25 StartY=2 StartZ=0 EndX=3.25 EndY=6 EndZ=0
    g2: LineSegment StartX=3.25 StartY=6 StartZ=0 EndX=-3.25 EndY=6 EndZ=0
    g3: LineSegment StartX=-3.25 StartY=6 StartZ=0 EndX=-3.25 EndY=2 EndZ=0
  constraints (11):
    c: Coincident(g0,g1)
    c: Coincident(g1,g2)
    c: Coincident(g2,g3)
    c: Coincident(g3,g0)
    c: Horizontal(g0)
    c: Vertical(g1)
    c: Vertical(g3)
    c: DistanceY(g-1,g0) = 2
    c: DistanceY(g1,g1) = 4
    c: Symmetric(g2,g1,g-2)
    c: DistanceX(g2,g2) = 6.5
FEATURE [PartDesign::Pad] Pad485
  BaseFeature = -> Fillet149
  Length = 1
  Length2 = 100
  Profile = -> Sketch1327
  Type = 0
FEATURE [Sketcher::SketchObject] Sketch1328
  MapMode = 5
  Placement = pos=(0,21.15,0) rot=(0,0.707107,0.707107;3.14159rad)
  Support = -> [Pad485]
  sketch-geometry (4):
    g0: LineSegment StartX=-2.75 StartY=5.5 StartZ=0 EndX=2.75 EndY=5.5 EndZ=0
    g1: LineSegment StartX=2.75 StartY=5.5 StartZ=0 EndX=2.75 EndY=2.5 EndZ=0
    g2: LineSegment StartX=2.75 StartY=2.5 StartZ=0 EndX=-2.75 EndY=2.5 EndZ=0
    g3: LineSegment StartX=-2.75 StartY=2.5 StartZ=0 EndX=-2.75 EndY=5.5 EndZ=0
  constraints (11):
    c: Coincident(g0,g1)
    c: Coincident(g1,g2)
    c: Coincident(g2,g3)
    c: Coincident(g3,g0)
    c: Horizontal(g0)
    c: Vertical(g1)
    c: Vertical(g3)
    c: Symmetric(g1,g2,g-2)
    c: DistanceY(g1,g0) = 3
    c: DistanceY(g-1,g1) = 2.5
    c: DistanceX(g0,g0) = 5.5
FEATURE [PartDesign::Pad] Pad543
  BaseFeature = -> Pad485
  Length = 4
  Length2 = 100
  Profile = -> Sketch1328
  Type = 0
FEATURE [Sketcher::SketchObject] Sketch1302
  MapMode = 5
  Placement = pos=(0,0,0) rot=(1,0,0;3.14159rad)
  Support = -> [Pad543]
  sketch-geometry (4):
    g0: LineSegment StartX=-10 StartY=-20.15 StartZ=0 EndX=10 EndY=-20.15 EndZ=0
    g1: LineSegment StartX=10 StartY=-20.15 StartZ=0 EndX=10 EndY=20.15 EndZ=0
    g2: LineSegment StartX=10 StartY=20.15 StartZ=0 EndX=-10 EndY=20.15 EndZ=0
    g3: LineSegment StartX=-10 StartY=20.15 StartZ=0 EndX=-10 EndY=-20.15 EndZ=0
  constraints (10):
    c: Coincident(g0,g1)
    c: Coincident(g1,g2)
    c: Coincident(g2,g3)
    c: Coincident(g3,g0)
    c: Horizontal(g0)
    c: Vertical(g1)
    c: Symmetric(g2,g1,g-2)
    c: Symmetric(g0,g2,g-1)
    c: DistanceX(g2,g2) = 20
    c: DistanceY(g1,g1) = 40.3
FEATURE [PartDesign::Pad] Pad474
  BaseFeature = -> Pad543
  Length = 2
  Length2 = 100
  Profile = -> Sketch1302
  Type = 0
FEATURE [PartDesign::Pad] Pad559  label="M3x20 Thread044"
  BaseFeature = -> Pad535
  Length = 20
  Length2 = 100
  Profile = -> Sketch1325
  Type = 0
FEATURE [Sketcher::SketchObject] Sketch1161
  MapMode = 5
  Placement = pos=(0,0,0) rot=(1,0,0;3.14159rad)
  Support = -> [Pad559]
  sketch-geometry (7):
    g0: LineSegment StartX=1.275 StartY=0.736122 StartZ=0 EndX=0 EndY=1.47224 EndZ=0
    g1: LineSegment StartX=0 StartY=1.47224 StartZ=0 EndX=-1.275 EndY=0.736122 EndZ=0
    g2: LineSegment StartX=-1.275 StartY=0.736122 StartZ=0 EndX=-1.275 EndY=-0.736122 EndZ=0
    g3: LineSegment StartX=-1.275 StartY=-0.736122 StartZ=0 EndX=1.34766e-11 EndY=-1.47224 EndZ=0
    g4: LineSegment StartX=1.34766e-11 StartY=-1.47224 StartZ=0 EndX=1.275 EndY=-0.736122 EndZ=0
    g5: LineSegment StartX=1.275 StartY=-0.736122 StartZ=0 EndX=1.275 EndY=0.736122 EndZ=0
    g6: Circle [constr] CenterX=0 CenterY=0 CenterZ=0 NormalX=0 NormalY=0 NormalZ=1 AngleXU=0 Radius=1.47224
  constraints (16):
    c: Coincident(g0,g1)
    c: Coincident(g1,g2)
    c: Coincident(g2,g3)
    c: Coincident(g3,g4)
    c: Coincident(g4,g5)
    c: Coincident(g5,g0)
    c: Equal(g0, g1-g5) x5
    c: PointOnObject(g0,g6)
    c: PointOnObject(g1,g6)
    c: PointOnObject(g2,g6)
    c: PointOnObject(g3,g6)
    c: PointOnObject(g4,g6)
    c: PointOnObject(g5,g6)
    c: Coincident(g6,g-1)
    c: PointOnObject(g0,g-2)
    c: DistanceX(g1,g0) = 2.55
FEATURE [PartDesign::Pocket] Pocket499  label="M3x20 Wrench041"
  BaseFeature = -> Pad559
  Length = 1.3
  Length2 = 100
  Profile = -> Sketch1161
  Type = 0
FEATURE [PartDesign::Pocket] Pocket507  label="M3x20 Wrench043"
  BaseFeature = -> Pad550
  Length = 1.3
  Length2 = 100
  Profile = -> Sketch1339
  Type = 0
FEATURE [PartDesign::Pocket] Pocket508  label="Screwholes005"
  BaseFeature = -> Pocket472
  Length = 15
  Length2 = 15
  Placement = pos=(0,0,0) rot=(1,0,0;1.5708rad)
  Profile = -> Sketch1354
  Type = 4
FEATURE [Sketcher::SketchObject] Sketch1341
  ExternalGeometry = -> [Pocket508]
  MapMode = 5
  Placement = pos=(0,14,-6.2e-15) rot=(-1,0,0;1.5708rad)
  Support = -> [Pocket508]
  sketch-geometry (1):
    g0: Circle CenterX=0 CenterY=-3.34863 CenterZ=0 NormalX=0 NormalY=0 NormalZ=1 AngleXU=0 Radius=2.85
  constraints (2):
    c: Coincident(g0,g-3)
    c: Radius(g0) = 2.85
FEATURE [PartDesign::Pocket] Pocket489  label="Screwhead Left002"
  BaseFeature = -> Pocket508
  Length = 2.5
  Length2 = 100
  Placement = pos=(0,0,0) rot=(1,0,0;1.5708rad)
  Profile = -> Sketch1341
  Type = 0
FEATURE [Sketcher::SketchObject] Sketch1363
  ExternalGeometry = -> [Pocket489]
  MapMode = 5
  Placement = pos=(0,-14,6.2e-15) rot=(1,0,0;1.5708rad)
  Support = -> [Pocket489]
  sketch-geometry (1):
    g0: Circle CenterX=0 CenterY=3.34863 CenterZ=0 NormalX=0 NormalY=0 NormalZ=1 AngleXU=0 Radius=2.85
  constraints (2):
    c: Coincident(g-3,g0)
    c: Radius(g0) = 2.85
FEATURE [PartDesign::Pocket] Pocket491  label="Screwhead Right002"
  BaseFeature = -> Pocket489
  Length = 2.5
  Length2 = 100
  Placement = pos=(0,0,0) rot=(1,0,0;1.5708rad)
  Profile = -> Sketch1363
  Type = 0
FEATURE [PartDesign::Body] Body326  label="Foot_Tip002"
  Group = -> [Sketch1349,Pad520,Sketch1338,Groove109,Sketch1163,SubtractivePipe012,PolarPattern002,Sketch1352,Groove105,Sketch1278,Pocket483,Sketch1358,Pocket479,Sketch1353,Pocket472,Sketch1354,Pocket508,Sketch1341,Pocket489,Sketch1363,Pocket491]
  Origin = -> Origin477
  Placement = pos=(0.75,0,37.62) rot=(0,1,0;3.14159rad)
  Tip = -> Pocket491
FEATURE [PartDesign::Revolution] Revolution027
  Angle = 360
  Axis = (0,2e-16,1)
  Base = (0,0,0)
  Placement = pos=(0,0,0) rot=(1,0,0;1.5708rad)
  Profile = -> Sketch1231
  ReferenceAxis = -> Sketch1231 [V_Axis]
FEATURE [PartDesign::Fillet] Fillet162
  Base = -> Revolution027 [Face2,Face6,Edge1,Edge11,Face4]
  BaseFeature = -> Revolution027
  Placement = pos=(0,0,0) rot=(1,0,0;1.5708rad)
  Radius = 0.25
FEATURE [PartDesign::Body] Body356  label="Rubber Dampener024"
  Group = -> [Sketch1231,Revolution027,Fillet162]
  Origin = -> Origin455
  Placement = pos=(-55.25,-12.25,100.75) rot=(-1,0,0;1.5708rad)
  Tip = -> Fillet162
FEATURE [PartDesign::Pad] Pad563  label="M3x20 Head046"
  Length = 3
  Length2 = 100
  Profile = -> Sketch1216
  Type = 0
FEATURE [Sketcher::SketchObject] Sketch1229
  MapMode = 5
  Placement = pos=(0,0,3) rot=(0,0,1;0rad)
  Support = -> [Pad563]
  sketch-geometry (1):
    g0: Circle CenterX=0 CenterY=0 CenterZ=0 NormalX=0 NormalY=0 NormalZ=1 AngleXU=0 Radius=1.5
  constraints (2):
    c: Coincident(g0,g-1)
    c: Radius(g0) = 1.5
FEATURE [PartDesign::Pad] Pad566  label="M3 Nut Primitive111"
  Length = 1.2
  Length2 = 1.2
  Profile = -> Sketch1219
  Type = 4
FEATURE [Sketcher::SketchObject] Sketch1203
  ExternalGeometry = -> [Pad566]
  MapMode = 5
  Placement = pos=(0,0,0) rot=(0.57735,0.57735,0.57735;2.0944rad)
  Support = -> [YZ_Plane427]
  sketch-geometry (6):
    g0: LineSegment StartX=-2.67543 StartY=1.2 StartZ=0 EndX=-3.67543 EndY=1.2 EndZ=0
    g1: LineSegment StartX=-3.67543 StartY=1.2 StartZ=0 EndX=-3.67543 EndY=-1.2 EndZ=0
    g2: LineSegment StartX=-3.67543 StartY=-1.2 StartZ=0 EndX=-2.67543 EndY=-1.2 EndZ=0
    g3: LineSegment StartX=-2.67543 StartY=-1.2 StartZ=0 EndX=-3.17543 EndY=-1 EndZ=0
    g4: LineSegment StartX=-3.17543 StartY=-1 StartZ=0 EndX=-3.17543 EndY=1 EndZ=0
    g5: LineSegment StartX=-3.17543 StartY=1 StartZ=0 EndX=-2.67543 EndY=1.2 EndZ=0
  constraints (15):
    c: Horizontal(g0)
    c: Coincident(g0,g1)
    c: Coincident(g1,g2)
    c: Coincident(g2,g3)
    c: Coincident(g3,g4)
    c: Coincident(g4,g5)
    c: Coincident(g5,g0)
    c: Symmetric(g4,g3,g-1)
    c: Symmetric(g0,g2,g-1)
    c: Symmetric(g1,g0,g-1)
    c: DistanceX(g0,g4) = 0.5
    c: DistanceY(g3,g4) = 2
    c: DistanceY(g1,g0) = 2.4
    c: PointOnObject(g3,g-3)
    c: DistanceX(g4,g0) = 0.5
FEATURE [PartDesign::Groove] Groove114  label="M3 Nut Smooth108"
  Angle = 360
  Axis = (-2e-16,3e-16,1)
  Base = (0,0,0)
  BaseFeature = -> Pad555
  Profile = -> Sketch1217
  ReferenceAxis = -> Sketch1217 [V_Axis]
  Reversed = true
FEATURE [PartDesign::Pad] Pad568  label="M3x20 Head047"
  Length = 3
  Length2 = 100
  Profile = -> Sketch1235
  Type = 0
FEATURE [PartDesign::Revolution] Revolution030
  Angle = 360
  Axis = (0,2e-16,1)
  Base = (0,0,0)
  Placement = pos=(0,0,0) rot=(1,0,0;1.5708rad)
  Profile = -> Sketch1237
  ReferenceAxis = -> Sketch1237 [V_Axis]
FEATURE [PartDesign::Fillet] Fillet174
  Base = -> Revolution030 [Face2,Face6,Edge1,Edge11,Face4]
  BaseFeature = -> Revolution030
  Placement = pos=(0,0,0) rot=(1,0,0;1.5708rad)
  Radius = 0.25
FEATURE [PartDesign::Body] Body394  label="Rubber Dampener033"
  Group = -> [Sketch1237,Revolution030,Fillet174]
  Origin = -> Origin469
  Placement = pos=(-89.5,-12.25,134.7) rot=(-1,0,0;1.5708rad)
  Tip = -> Fillet174
FEATURE [PartDesign::Pad] Pad570
  Length = 10
  Length2 = 100
  Placement = pos=(0,0,0) rot=(1,0,0;1.5708rad)
  Profile = -> Sketch1210
  Reversed = true
  Type = 0
FEATURE [PartDesign::Body] Body373  label="red wire011"
  Group = -> [Sketch1210,Pad570]
  Origin = -> Origin541
  Placement = pos=(0,25.15,0) rot=(0,0,1;0rad)
  Tip = -> Pad570
FEATURE [PartDesign::Revolution] Revolution033
  Angle = 360
  Axis = (0,2e-16,1)
  Base = (0,0,0)
  Placement = pos=(0,0,0) rot=(1,0,0;1.5708rad)
  Profile = -> Sketch1233
  ReferenceAxis = -> Sketch1233 [V_Axis]
FEATURE [PartDesign::Fillet] Fillet164
  Base = -> Revolution033 [Face2,Face6,Edge1,Edge11,Face4]
  BaseFeature = -> Revolution033
  Placement = pos=(0,0,0) rot=(1,0,0;1.5708rad)
  Radius = 0.25
FEATURE [PartDesign::Body] Body374  label="Rubber Dampener029"
  Group = -> [Sketch1233,Revolution033,Fillet164]
  Origin = -> Origin497
  Placement = pos=(-96.5,-12.25,127.7) rot=(-1,0,0;1.5708rad)
  Tip = -> Fillet164
FEATURE [PartDesign::Pad] Pad575
  BaseFeature = -> Pad547
  Length = 2.5
  Length2 = 100
  Profile = -> Sketch1208
  Type = 0
FEATURE [Sketcher::SketchObject] Sketch1195
  MapMode = 5
  Placement = pos=(0,0,29.1) rot=(0,0,1;0rad)
  Support = -> [Pad575]
  sketch-geometry (4):
    g0: LineSegment StartX=-10 StartY=-20.15 StartZ=0 EndX=10 EndY=-20.15 EndZ=0
    g1: LineSegment StartX=10 StartY=-20.15 StartZ=0 EndX=10 EndY=20.15 EndZ=0
    g2: LineSegment StartX=10 StartY=20.15 StartZ=0 EndX=-10 EndY=20.15 EndZ=0
    g3: LineSegment StartX=-10 StartY=20.15 StartZ=0 EndX=-10 EndY=-20.15 EndZ=0
  constraints (10):
    c: Coincident(g0,g1)
    c: Coincident(g1,g2)
    c: Coincident(g2,g3)
    c: Coincident(g3,g0)
    c: Horizontal(g0)
    c: Vertical(g3)
    c: Symmetric(g1,g2,g-2)
    c: Symmetric(g1,g0,g-1)
    c: DistanceX(g2,g2) = 20
    c: DistanceY(g1,g1) = 40.3
FEATURE [PartDesign::Revolution] Revolution035
  Angle = 360
  Axis = (0,2e-16,1)
  Base = (0,0,0)
  Placement = pos=(0,0,0) rot=(1,0,0;1.5708rad)
  Profile = -> Sketch1121
  ReferenceAxis = -> Sketch1121 [V_Axis]
FEATURE [PartDesign::Fillet] Fillet170
  Base = -> Revolution035 [Face2,Face6,Edge1,Edge11,Face4]
  BaseFeature = -> Revolution035
  Placement = pos=(0,0,0) rot=(1,0,0;1.5708rad)
  Radius = 0.25
FEATURE [PartDesign::Body] Body369  label="Rubber Dampener028"
  Group = -> [Sketch1121,Revolution035,Fillet170]
  Origin = -> Origin470
  Placement = pos=(-62.3,-12.25,93.7) rot=(-1,0,0;1.5708rad)
  Tip = -> Fillet170
FEATURE [PartDesign::Pad] Pad597
  Length = 2
  Length2 = 100
  Profile = -> Sketch1256
  Type = 0
FEATURE [PartDesign::Pad] Pad598  label="M3x8 Head066"
  Length = 2
  Length2 = 100
  Profile = -> Sketch1253
  Type = 0
FEATURE [Sketcher::SketchObject] Sketch1228
  MapMode = 5
  Placement = pos=(0,0,2) rot=(0,0,1;0rad)
  Support = -> [Pad598]
  sketch-geometry (1):
    g0: Circle CenterX=0 CenterY=0 CenterZ=0 NormalX=0 NormalY=0 NormalZ=1 AngleXU=0 Radius=1
  constraints (2):
    c: Coincident(g0,g-1)
    c: Radius(g0) = 1
FEATURE [PartDesign::Pad] Pad603  label="M3x8 Head068"
  Length = 2
  Length2 = 100
  Profile = -> Sketch1181
  Type = 0
FEATURE [PartDesign::Pad] Pad612  label="M3x8 Thread070"
  BaseFeature = -> Pad598
  Length = 8
  Length2 = 100
  Profile = -> Sketch1228
  Type = 0
FEATURE [Sketcher::SketchObject] Sketch1254
  MapMode = 5
  Placement = pos=(0,0,0) rot=(1,0,0;3.14159rad)
  Support = -> [Pad612]
  sketch-geometry (7):
    g0: LineSegment StartX=0.77 StartY=0.44456 StartZ=0 EndX=0 EndY=0.889119 EndZ=0
    g1: LineSegment StartX=0 StartY=0.889119 StartZ=0 EndX=-0.77 EndY=0.44456 EndZ=0
    g2: LineSegment StartX=-0.77 StartY=0.44456 StartZ=0 EndX=-0.77 EndY=-0.44456 EndZ=0
    g3: LineSegment StartX=-0.77 StartY=-0.44456 StartZ=0 EndX=3.85628e-11 EndY=-0.889119 EndZ=0
    g4: LineSegment StartX=3.85628e-11 StartY=-0.889119 StartZ=0 EndX=0.77 EndY=-0.44456 EndZ=0
    g5: LineSegment StartX=0.77 StartY=-0.44456 StartZ=0 EndX=0.77 EndY=0.44456 EndZ=0
    g6: Circle [constr] CenterX=0 CenterY=0 CenterZ=0 NormalX=0 NormalY=0 NormalZ=1 AngleXU=0 Radius=0.889119
  constraints (16):
    c: Coincident(g0,g1)
    c: Coincident(g1,g2)
    c: Coincident(g2,g3)
    c: Coincident(g3,g4)
    c: Coincident(g4,g5)
    c: Coincident(g5,g0)
    c: Equal(g0, g1-g5) x5
    c: PointOnObject(g0,g6)
    c: PointOnObject(g1,g6)
    c: PointOnObject(g2,g6)
    c: PointOnObject(g3,g6)
    c: PointOnObject(g4,g6)
    c: PointOnObject(g5,g6)
    c: Coincident(g6,g-1)
    c: PointOnObject(g0,g-2)
    c: DistanceX(g1,g0) = 1.54
FEATURE [PartDesign::Pad] Pad614  label="M3x8 Head070"
  Length = 3
  Length2 = 100
  Profile = -> Sketch1262
  Type = 0
FEATURE [Sketcher::SketchObject] Sketch1175
  MapMode = 5
  Placement = pos=(0,0,3) rot=(0,0,1;0rad)
  Support = -> [Pad614]
  sketch-geometry (1):
    g0: Circle CenterX=0 CenterY=0 CenterZ=0 NormalX=0 NormalY=0 NormalZ=1 AngleXU=0 Radius=1.5
  constraints (2):
    c: Coincident(g0,g-1)
    c: Radius(g0) = 1.5
FEATURE [PartDesign::Pad] Pad605  label="M3x8 Thread068"
  BaseFeature = -> Pad614
  Length = 8
  Length2 = 100
  Profile = -> Sketch1175
  Type = 0
FEATURE [Sketcher::SketchObject] Sketch1191
  MapMode = 5
  Placement = pos=(0,0,0) rot=(1,0,0;3.14159rad)
  Support = -> [Pad605]
  sketch-geometry (7):
    g0: LineSegment StartX=1.275 StartY=0.736122 StartZ=0 EndX=0 EndY=1.47224 EndZ=0
    g1: LineSegment StartX=0 StartY=1.47224 StartZ=0 EndX=-1.275 EndY=0.736122 EndZ=0
    g2: LineSegment StartX=-1.275 StartY=0.736122 StartZ=0 EndX=-1.275 EndY=-0.736122 EndZ=0
    g3: LineSegment StartX=-1.275 StartY=-0.736122 StartZ=0 EndX=1.34766e-11 EndY=-1.47224 EndZ=0
    g4: LineSegment StartX=1.34766e-11 StartY=-1.47224 StartZ=0 EndX=1.275 EndY=-0.736122 EndZ=0
    g5: LineSegment StartX=1.275 StartY=-0.736122 StartZ=0 EndX=1.275 EndY=0.736122 EndZ=0
    g6: Circle [constr] CenterX=0 CenterY=0 CenterZ=0 NormalX=0 NormalY=0 NormalZ=1 AngleXU=0 Radius=1.47224
  constraints (16):
    c: Coincident(g0,g1)
    c: Coincident(g1,g2)
    c: Coincident(g2,g3)
    c: Coincident(g3,g4)
    c: Coincident(g4,g5)
    c: Coincident(g5,g0)
    c: Equal(g0, g1-g5) x5
    c: PointOnObject(g0,g6)
    c: PointOnObject(g1,g6)
    c: PointOnObject(g2,g6)
    c: PointOnObject(g3,g6)
    c: PointOnObject(g4,g6)
    c: PointOnObject(g5,g6)
    c: Coincident(g6,g-1)
    c: PointOnObject(g0,g-2)
    c: DistanceX(g1,g0) = 2.55
FEATURE [PartDesign::Pocket] Pocket527  label="M3x8 Wrench067"
  BaseFeature = -> Pad605
  Length = 1.3
  Length2 = 100
  Profile = -> Sketch1191
  Type = 0
FEATURE [PartDesign::Pad] Pad615  label="M3x8 Head071"
  Length = 3
  Length2 = 100
  Profile = -> Sketch1192
  Type = 0
FEATURE [Sketcher::SketchObject] Sketch1182
  MapMode = 5
  Placement = pos=(0,0,3) rot=(0,0,1;0rad)
  Support = -> [Pad615]
  sketch-geometry (1):
    g0: Circle CenterX=0 CenterY=0 CenterZ=0 NormalX=0 NormalY=0 NormalZ=1 AngleXU=0 Radius=1.5
  constraints (2):
    c: Coincident(g0,g-1)
    c: Radius(g0) = 1.5
FEATURE [PartDesign::Pad] Pad611  label="M3x8 Thread069"
  BaseFeature = -> Pad615
  Length = 8
  Length2 = 100
  Profile = -> Sketch1182
  Type = 0
FEATURE [Sketcher::SketchObject] Sketch1186
  MapMode = 5
  Placement = pos=(0,0,0) rot=(1,0,0;3.14159rad)
  Support = -> [Pad611]
  sketch-geometry (7):
    g0: LineSegment StartX=1.275 StartY=0.736122 StartZ=0 EndX=0 EndY=1.47224 EndZ=0
    g1: LineSegment StartX=0 StartY=1.47224 StartZ=0 EndX=-1.275 EndY=0.736122 EndZ=0
    g2: LineSegment StartX=-1.275 StartY=0.736122 StartZ=0 EndX=-1.275 EndY=-0.736122 EndZ=0
    g3: LineSegment StartX=-1.275 StartY=-0.736122 StartZ=0 EndX=1.34766e-11 EndY=-1.47224 EndZ=0
    g4: LineSegment StartX=1.34766e-11 StartY=-1.47224 StartZ=0 EndX=1.275 EndY=-0.736122 EndZ=0
    g5: LineSegment StartX=1.275 StartY=-0.736122 StartZ=0 EndX=1.275 EndY=0.736122 EndZ=0
    g6: Circle [constr] CenterX=0 CenterY=0 CenterZ=0 NormalX=0 NormalY=0 NormalZ=1 AngleXU=0 Radius=1.47224
  constraints (16):
    c: Coincident(g0,g1)
    c: Coincident(g1,g2)
    c: Coincident(g2,g3)
    c: Coincident(g3,g4)
    c: Coincident(g4,g5)
    c: Coincident(g5,g0)
    c: Equal(g0, g1-g5) x5
    c: PointOnObject(g0,g6)
    c: PointOnObject(g1,g6)
    c: PointOnObject(g2,g6)
    c: PointOnObject(g3,g6)
    c: PointOnObject(g4,g6)
    c: PointOnObject(g5,g6)
    c: Coincident(g6,g-1)
    c: PointOnObject(g0,g-2)
    c: DistanceX(g1,g0) = 2.55
FEATURE [PartDesign::Pocket] Pocket540  label="M3x8 Wrench073"
  BaseFeature = -> Pad612
  Length = 1
  Length2 = 100
  Profile = -> Sketch1254
  Type = 0
FEATURE [PartDesign::Pad] Pad616  label="M3x8 Head072"
  Length = 3
  Length2 = 100
  Profile = -> Sketch1183
  Type = 0
FEATURE [Sketcher::SketchObject] Sketch1197
  MapMode = 5
  Placement = pos=(0,0,3) rot=(0,0,1;0rad)
  Support = -> [Pad616]
  sketch-geometry (1):
    g0: Circle CenterX=0 CenterY=0 CenterZ=0 NormalX=0 NormalY=0 NormalZ=1 AngleXU=0 Radius=1.5
  constraints (2):
    c: Coincident(g0,g-1)
    c: Radius(g0) = 1.5
FEATURE [PartDesign::Pad] Pad618  label="M3x8 Head073"
  Length = 2
  Length2 = 100
  Profile = -> Sketch1258
  Type = 0
FEATURE [PartDesign::Pad] Pad625  label="M3x8 Thread074"
  BaseFeature = -> Pad616
  Length = 8
  Length2 = 100
  Profile = -> Sketch1197
  Type = 0
FEATURE [Sketcher::SketchObject] Sketch1264
  MapMode = 5
  Placement = pos=(0,0,0) rot=(1,0,0;3.14159rad)
  Support = -> [Pad625]
  sketch-geometry (7):
    g0: LineSegment StartX=1.275 StartY=0.736122 StartZ=0 EndX=0 EndY=1.47224 EndZ=0
    g1: LineSegment StartX=0 StartY=1.47224 StartZ=0 EndX=-1.275 EndY=0.736122 EndZ=0
    g2: LineSegment StartX=-1.275 StartY=0.736122 StartZ=0 EndX=-1.275 EndY=-0.736122 EndZ=0
    g3: LineSegment StartX=-1.275 StartY=-0.736122 StartZ=0 EndX=1.34766e-11 EndY=-1.47224 EndZ=0
    g4: LineSegment StartX=1.34766e-11 StartY=-1.47224 StartZ=0 EndX=1.275 EndY=-0.736122 EndZ=0
    g5: LineSegment StartX=1.275 StartY=-0.736122 StartZ=0 EndX=1.275 EndY=0.736122 EndZ=0
    g6: Circle [constr] CenterX=0 CenterY=0 CenterZ=0 NormalX=0 NormalY=0 NormalZ=1 AngleXU=0 Radius=1.47224
  constraints (16):
    c: Coincident(g0,g1)
    c: Coincident(g1,g2)
    c: Coincident(g2,g3)
    c: Coincident(g3,g4)
    c: Coincident(g4,g5)
    c: Coincident(g5,g0)
    c: Equal(g0, g1-g5) x5
    c: PointOnObject(g0,g6)
    c: PointOnObject(g1,g6)
    c: PointOnObject(g2,g6)
    c: PointOnObject(g3,g6)
    c: PointOnObject(g4,g6)
    c: PointOnObject(g5,g6)
    c: Coincident(g6,g-1)
    c: PointOnObject(g0,g-2)
    c: DistanceX(g1,g0) = 2.55
FEATURE [PartDesign::Pocket] Pocket546  label="M3x8 Wrench076"
  BaseFeature = -> Pad625
  Length = 1.3
  Length2 = 100
  Profile = -> Sketch1264
  Type = 0
FEATURE [PartDesign::Pad] Pad626  label="Baseplate027"
  Length = 5
  Length2 = 100
  Profile = -> Sketch1239
  Type = 0
FEATURE [PartDesign::Pad] Pad613  label="Baseplate Expansion002"
  BaseFeature = -> Pad626
  Length = 20
  Length2 = 100
  Profile = -> Pad626 [Face10]
  Type = 0
FEATURE [Sketcher::SketchObject] Sketch1252
  MapMode = 5
  Placement = pos=(0,0,25) rot=(0,0,1;0rad)
  Support = -> [Pad613]
  sketch-geometry (8):
    g0: LineSegment StartX=9.75 StartY=28.25 StartZ=0 EndX=9.75 EndY=20.25 EndZ=0
    g1: LineSegment StartX=9.75 StartY=20.25 StartZ=0 EndX=-18.75 EndY=20.25 EndZ=0
    g2: LineSegment StartX=-18.75 StartY=20.25 StartZ=0 EndX=-18.75 EndY=-20.25 EndZ=0
    g3: LineSegment StartX=-18.75 StartY=-20.25 StartZ=0 EndX=9.75 EndY=-20.25 EndZ=0
    g4: LineSegment StartX=9.75 StartY=-20.25 StartZ=0 EndX=9.75 EndY=-28.25 EndZ=0
    g5: LineSegment StartX=9.75 StartY=-28.25 StartZ=0 EndX=21.75 EndY=-28.25 EndZ=0
    g6: LineSegment StartX=21.75 StartY=-28.25 StartZ=0 EndX=21.75 EndY=28.25 EndZ=0
    g7: LineSegment StartX=21.75 StartY=28.25 StartZ=0 EndX=9.75 EndY=28.25 EndZ=0
  constraints (22):
    c: Vertical(g0)
    c: Coincident(g0,g1)
    c: Horizontal(g1)
    c: Coincident(g1,g2)
    c: Coincident(g2,g3)
    c: Horizontal(g3)
    c: Coincident(g3,g4)
    c: Vertical(g4)
    c: Coincident(g4,g5)
    c: Horizontal(g5)
    c: Coincident(g5,g6)
    c: Coincident(g6,g7)
    c: Coincident(g7,g0)
    c: Horizontal(g7)
    c: Equal(g7,g5)
    c: Symmetric(g6,g5,g-1)
    c: Symmetric(g1,g2,g-1)
    c: DistanceY(g6,g6) = 56.5
    c: DistanceX(g-1,g6) = 21.75
    c: DistanceX(g1,g-1) = 18.75
    c: DistanceY(g0,g0) = 8
    c: DistanceX(g1,g0) = 28.5
FEATURE [PartDesign::Pocket] Pocket544  label="Servo Pocket010"
  BaseFeature = -> Pad613
  Length = 20
  Length2 = 100
  Profile = -> Sketch1252
  Type = 0
FEATURE [Sketcher::SketchObject] Sketch1246
  MapMode = 5
  Placement = pos=(0,0,5) rot=(0,0,1;0rad)
  Support = -> [Pocket544]
  sketch-geometry (1):
    g0: Circle CenterX=0 CenterY=0 CenterZ=0 NormalX=0 NormalY=0 NormalZ=1 AngleXU=0 Radius=16.5
  constraints (2):
    c: Coincident(g0,g-1)
    c: Radius(g0) = 16.5
FEATURE [PartDesign::Pocket] Pocket538  label="Accesshole Servohorn Cap002"
  BaseFeature = -> Pocket544
  Length = 5
  Length2 = 100
  Profile = -> Sketch1246
  Type = 0
FEATURE [PartDesign::Pad] Pad629  label="M3 Nut Primitive118"
  Length = 1.2
  Length2 = 1.2
  Profile = -> Sketch1267
  Type = 4
FEATURE [Sketcher::SketchObject] Sketch1193
  ExternalGeometry = -> [Pad629]
  MapMode = 5
  Placement = pos=(0,0,0) rot=(0.57735,0.57735,0.57735;2.0944rad)
  Support = -> [YZ_Plane414]
  sketch-geometry (6):
    g0: LineSegment StartX=-2.67543 StartY=1.2 StartZ=0 EndX=-3.67543 EndY=1.2 EndZ=0
    g1: LineSegment StartX=-3.67543 StartY=1.2 StartZ=0 EndX=-3.67543 EndY=-1.2 EndZ=0
    g2: LineSegment StartX=-3.67543 StartY=-1.2 StartZ=0 EndX=-2.67543 EndY=-1.2 EndZ=0
    g3: LineSegment StartX=-2.67543 StartY=-1.2 StartZ=0 EndX=-3.17543 EndY=-1 EndZ=0
    g4: LineSegment StartX=-3.17543 StartY=-1 StartZ=0 EndX=-3.17543 EndY=1 EndZ=0
    g5: LineSegment StartX=-3.17543 StartY=1 StartZ=0 EndX=-2.67543 EndY=1.2 EndZ=0
  constraints (15):
    c: Horizontal(g0)
    c: Coincident(g0,g1)
    c: Coincident(g1,g2)
    c: Coincident(g2,g3)
    c: Coincident(g3,g4)
    c: Coincident(g4,g5)
    c: Coincident(g5,g0)
    c: Symmetric(g4,g3,g-1)
    c: Symmetric(g0,g2,g-1)
    c: Symmetric(g1,g0,g-1)
    c: DistanceX(g0,g4) = 0.5
    c: DistanceY(g3,g4) = 2
    c: DistanceY(g1,g0) = 2.4
    c: PointOnObject(g3,g-3)
    c: DistanceX(g4,g0) = 0.5
FEATURE [PartDesign::Pocket] Pocket549  label="M3x8 Wrench077"
  BaseFeature = -> Pad611
  Length = 1.3
  Length2 = 100
  Profile = -> Sketch1186
  Type = 0
FEATURE [PartDesign::Chamfer] Chamfer240  label="M3x8 Smooth063"
  Base = -> Pocket549 [Face11,Edge2,Edge24,Edge3]
  BaseFeature = -> Pocket549
  Size = 0.2
FEATURE [PartDesign::Groove] Groove129  label="M3 Nut Smooth123"
  Angle = 360
  Axis = (-2e-16,3e-16,1)
  Base = (0,0,0)
  BaseFeature = -> Pad629
  Profile = -> Sketch1193
  ReferenceAxis = -> Sketch1193 [V_Axis]
  Reversed = true
FEATURE [PartDesign::Pad] Pad634  label="M3x8 Head078"
  Length = 3
  Length2 = 100
  Profile = -> Sketch1213
  Type = 0
FEATURE [Sketcher::SketchObject] Sketch1189
  MapMode = 5
  Placement = pos=(0,0,3) rot=(0,0,1;0rad)
  Support = -> [Pad634]
  sketch-geometry (1):
    g0: Circle CenterX=0 CenterY=0 CenterZ=0 NormalX=0 NormalY=0 NormalZ=1 AngleXU=0 Radius=1.5
  constraints (2):
    c: Coincident(g0,g-1)
    c: Radius(g0) = 1.5
FEATURE [PartDesign::Pad] Pad630  label="M3x8 Thread075"
  BaseFeature = -> Pad634
  Length = 8
  Length2 = 100
  Profile = -> Sketch1189
  Type = 0
FEATURE [Sketcher::SketchObject] Sketch1201
  MapMode = 5
  Placement = pos=(0,0,0) rot=(1,0,0;3.14159rad)
  Support = -> [Pad630]
  sketch-geometry (7):
    g0: LineSegment StartX=1.275 StartY=0.736122 StartZ=0 EndX=0 EndY=1.47224 EndZ=0
    g1: LineSegment StartX=0 StartY=1.47224 StartZ=0 EndX=-1.275 EndY=0.736122 EndZ=0
    g2: LineSegment StartX=-1.275 StartY=0.736122 StartZ=0 EndX=-1.275 EndY=-0.736122 EndZ=0
    g3: LineSegment StartX=-1.275 StartY=-0.736122 StartZ=0 EndX=1.34766e-11 EndY=-1.47224 EndZ=0
    g4: LineSegment StartX=1.34766e-11 StartY=-1.47224 StartZ=0 EndX=1.275 EndY=-0.736122 EndZ=0
    g5: LineSegment StartX=1.275 StartY=-0.736122 StartZ=0 EndX=1.275 EndY=0.736122 EndZ=0
    g6: Circle [constr] CenterX=0 CenterY=0 CenterZ=0 NormalX=0 NormalY=0 NormalZ=1 AngleXU=0 Radius=1.47224
  constraints (16):
    c: Coincident(g0,g1)
    c: Coincident(g1,g2)
    c: Coincident(g2,g3)
    c: Coincident(g3,g4)
    c: Coincident(g4,g5)
    c: Coincident(g5,g0)
    c: Equal(g0, g1-g5) x5
    c: PointOnObject(g0,g6)
    c: PointOnObject(g1,g6)
    c: PointOnObject(g2,g6)
    c: PointOnObject(g3,g6)
    c: PointOnObject(g4,g6)
    c: PointOnObject(g5,g6)
    c: Coincident(g6,g-1)
    c: PointOnObject(g0,g-2)
    c: DistanceX(g1,g0) = 2.55
FEATURE [PartDesign::Pad] Pad635  label="M3 Nut Primitive120"
  Length = 1.2
  Length2 = 1.2
  Profile = -> Sketch1270
  Type = 4
FEATURE [Sketcher::SketchObject] Sketch1185
  ExternalGeometry = -> [Pad635]
  MapMode = 5
  Placement = pos=(0,0,0) rot=(0.57735,0.57735,0.57735;2.0944rad)
  Support = -> [YZ_Plane422]
  sketch-geometry (6):
    g0: LineSegment StartX=-2.67543 StartY=1.2 StartZ=0 EndX=-3.67543 EndY=1.2 EndZ=0
    g1: LineSegment StartX=-3.67543 StartY=1.2 StartZ=0 EndX=-3.67543 EndY=-1.2 EndZ=0
    g2: LineSegment StartX=-3.67543 StartY=-1.2 StartZ=0 EndX=-2.67543 EndY=-1.2 EndZ=0
    g3: LineSegment StartX=-2.67543 StartY=-1.2 StartZ=0 EndX=-3.17543 EndY=-1 EndZ=0
    g4: LineSegment StartX=-3.17543 StartY=-1 StartZ=0 EndX=-3.17543 EndY=1 EndZ=0
    g5: LineSegment StartX=-3.17543 StartY=1 StartZ=0 EndX=-2.67543 EndY=1.2 EndZ=0
  constraints (15):
    c: Horizontal(g0)
    c: Coincident(g0,g1)
    c: Coincident(g1,g2)
    c: Coincident(g2,g3)
    c: Coincident(g3,g4)
    c: Coincident(g4,g5)
    c: Coincident(g5,g0)
    c: Symmetric(g4,g3,g-1)
    c: Symmetric(g0,g2,g-1)
    c: Symmetric(g1,g0,g-1)
    c: DistanceX(g0,g4) = 0.5
    c: DistanceY(g3,g4) = 2
    c: DistanceY(g1,g0) = 2.4
    c: PointOnObject(g3,g-3)
    c: DistanceX(g4,g0) = 0.5
FEATURE [PartDesign::Groove] Groove122  label="M3 Nut Smooth116"
  Angle = 360
  Axis = (-2e-16,3e-16,1)
  Base = (0,0,0)
  BaseFeature = -> Pad635
  Profile = -> Sketch1185
  ReferenceAxis = -> Sketch1185 [V_Axis]
  Reversed = true
FEATURE [PartDesign::Chamfer] Chamfer248  label="M3 Nut Smooth Hole104"
  Base = -> Groove122 [Edge24,Edge23]
  BaseFeature = -> Groove122
  Size = 0.2
FEATURE [PartDesign::Body] Body371  label="M3 Nut068"
  Group = -> [Sketch1270,Pad635,Sketch1185,Groove122,Chamfer248]
  Origin = -> Origin435
  Placement = pos=(-14.15,14.15,3.5) rot=(0,0,1;0.261799rad)
  Tip = -> Chamfer248
FEATURE [PartDesign::Pad] Pad636  label="M3 Nut Primitive121"
  Length = 0.6
  Length2 = 0.6
  Profile = -> Sketch1259
  Type = 4
FEATURE [Sketcher::SketchObject] Sketch1205
  ExternalGeometry = -> [Pad636]
  MapMode = 5
  Placement = pos=(0,0,0) rot=(0.57735,0.57735,0.57735;2.0944rad)
  Support = -> [YZ_Plane518]
  sketch-geometry (6):
    g0: LineSegment StartX=-1.9594 StartY=0.6 StartZ=0 EndX=-2.8094 EndY=0.6 EndZ=0
    g1: LineSegment StartX=-2.8094 StartY=0.6 StartZ=0 EndX=-2.8094 EndY=-0.6 EndZ=0
    g2: LineSegment StartX=-2.8094 StartY=-0.6 StartZ=0 EndX=-1.9594 EndY=-0.6 EndZ=0
    g3: LineSegment StartX=-1.9594 StartY=-0.6 StartZ=0 EndX=-2.3094 EndY=-0.4 EndZ=0
    g4: LineSegment StartX=-2.3094 StartY=-0.4 StartZ=0 EndX=-2.3094 EndY=0.4 EndZ=0
    g5: LineSegment StartX=-2.3094 StartY=0.4 StartZ=0 EndX=-1.9594 EndY=0.6 EndZ=0
  constraints (15):
    c: Horizontal(g0)
    c: Coincident(g0,g1)
    c: Coincident(g1,g2)
    c: Coincident(g2,g3)
    c: Coincident(g3,g4)
    c: Coincident(g4,g5)
    c: Coincident(g5,g0)
    c: Symmetric(g4,g3,g-1)
    c: Symmetric(g0,g2,g-1)
    c: Symmetric(g1,g0,g-1)
    c: DistanceX(g0,g4) = 0.5
    c: DistanceY(g3,g4) = 0.8
    c: DistanceY(g1,g0) = 1.2
    c: PointOnObject(g3,g-3)
    c: DistanceX(g4,g0) = 0.35
FEATURE [PartDesign::Groove] Groove124  label="M3 Nut Smooth118"
  Angle = 360
  Axis = (-2e-16,3e-16,1)
  Base = (0,0,0)
  BaseFeature = -> Pad636
  Profile = -> Sketch1205
  ReferenceAxis = -> Sketch1205 [V_Axis]
  Reversed = true
FEATURE [PartDesign::Chamfer] Chamfer222  label="M3 Nut Smooth Hole094"
  Base = -> Groove124 [Edge24,Edge23]
  BaseFeature = -> Groove124
  Size = 0.2
FEATURE [PartDesign::Body] Body342  label="M2 Nut047"
  Group = -> [Sketch1259,Pad636,Sketch1205,Groove124,Chamfer222,Sketch1241,Sketch1240]
  Origin = -> Origin420
  Placement = pos=(0,0,2.75) rot=(0,0,1;0rad)
  Tip = -> Chamfer222
FEATURE [PartDesign::Pad] Pad638
  Length = 10
  Length2 = 100
  Placement = pos=(0,0,0) rot=(1,0,0;1.5708rad)
  Profile = -> Sketch1209
  Reversed = true
  Type = 0
FEATURE [PartDesign::Pad] Pad639  label="M3 Nut Primitive122"
  Length = 0.6
  Length2 = 0.6
  Profile = -> Sketch1244
  Type = 4
FEATURE [PartDesign::Pad] Pad641  label="M3 Nut Primitive123"
  Length = 1.2
  Length2 = 1.2
  Profile = -> Sketch1269
  Type = 4
FEATURE [Sketcher::SketchObject] Sketch1255
  ExternalGeometry = -> [Pad641]
  MapMode = 5
  Placement = pos=(0,0,0) rot=(0.57735,0.57735,0.57735;2.0944rad)
  Support = -> [YZ_Plane433]
  sketch-geometry (6):
    g0: LineSegment StartX=-2.67543 StartY=1.2 StartZ=0 EndX=-3.67543 EndY=1.2 EndZ=0
    g1: LineSegment StartX=-3.67543 StartY=1.2 StartZ=0 EndX=-3.67543 EndY=-1.2 EndZ=0
    g2: LineSegment StartX=-3.67543 StartY=-1.2 StartZ=0 EndX=-2.67543 EndY=-1.2 EndZ=0
    g3: LineSegment StartX=-2.67543 StartY=-1.2 StartZ=0 EndX=-3.17543 EndY=-1 EndZ=0
    g4: LineSegment StartX=-3.17543 StartY=-1 StartZ=0 EndX=-3.17543 EndY=1 EndZ=0
    g5: LineSegment StartX=-3.17543 StartY=1 StartZ=0 EndX=-2.67543 EndY=1.2 EndZ=0
  constraints (15):
    c: Horizontal(g0)
    c: Coincident(g0,g1)
    c: Coincident(g1,g2)
    c: Coincident(g2,g3)
    c: Coincident(g3,g4)
    c: Coincident(g4,g5)
    c: Coincident(g5,g0)
    c: Symmetric(g4,g3,g-1)
    c: Symmetric(g0,g2,g-1)
    c: Symmetric(g1,g0,g-1)
    c: DistanceX(g0,g4) = 0.5
    c: DistanceY(g3,g4) = 2
    c: DistanceY(g1,g0) = 2.4
    c: PointOnObject(g3,g-3)
    c: DistanceX(g4,g0) = 0.5
FEATURE [PartDesign::Groove] Groove131  label="M3 Nut Smooth125"
  Angle = 360
  Axis = (-2e-16,3e-16,1)
  Base = (0,0,0)
  BaseFeature = -> Pad641
  Profile = -> Sketch1255
  ReferenceAxis = -> Sketch1255 [V_Axis]
  Reversed = true
FEATURE [PartDesign::Chamfer] Chamfer252  label="M3 Nut Smooth Hole106"
  Base = -> Groove131 [Edge24,Edge23]
  BaseFeature = -> Groove131
  Size = 0.2
FEATURE [PartDesign::Body] Body368  label="M3 Nut067"
  Group = -> [Sketch1269,Pad641,Sketch1255,Groove131,Chamfer252]
  Origin = -> Origin516
  Placement = pos=(-14.15,-14.15,3.5) rot=(0,0,-1;0.261799rad)
  Tip = -> Chamfer252
FEATURE [PartDesign::Pad] Pad643  label="M3 Nut Primitive124"
  Length = 1.2
  Length2 = 1.2
  Profile = -> Sketch1211
  Type = 4
FEATURE [Sketcher::SketchObject] Sketch1224
  ExternalGeometry = -> [Pad643]
  MapMode = 5
  Placement = pos=(0,0,0) rot=(0.57735,0.57735,0.57735;2.0944rad)
  Support = -> [YZ_Plane423]
  sketch-geometry (6):
    g0: LineSegment StartX=-2.67543 StartY=1.2 StartZ=0 EndX=-3.67543 EndY=1.2 EndZ=0
    g1: LineSegment StartX=-3.67543 StartY=1.2 StartZ=0 EndX=-3.67543 EndY=-1.2 EndZ=0
    g2: LineSegment StartX=-3.67543 StartY=-1.2 StartZ=0 EndX=-2.67543 EndY=-1.2 EndZ=0
    g3: LineSegment StartX=-2.67543 StartY=-1.2 StartZ=0 EndX=-3.17543 EndY=-1 EndZ=0
    g4: LineSegment StartX=-3.17543 StartY=-1 StartZ=0 EndX=-3.17543 EndY=1 EndZ=0
    g5: LineSegment StartX=-3.17543 StartY=1 StartZ=0 EndX=-2.67543 EndY=1.2 EndZ=0
  constraints (15):
    c: Horizontal(g0)
    c: Coincident(g0,g1)
    c: Coincident(g1,g2)
    c: Coincident(g2,g3)
    c: Coincident(g3,g4)
    c: Coincident(g4,g5)
    c: Coincident(g5,g0)
    c: Symmetric(g4,g3,g-1)
    c: Symmetric(g0,g2,g-1)
    c: Symmetric(g1,g0,g-1)
    c: DistanceX(g0,g4) = 0.5
    c: DistanceY(g3,g4) = 2
    c: DistanceY(g1,g0) = 2.4
    c: PointOnObject(g3,g-3)
    c: DistanceX(g4,g0) = 0.5
FEATURE [PartDesign::Groove] Groove130  label="M3 Nut Smooth124"
  Angle = 360
  Axis = (-2e-16,3e-16,1)
  Base = (0,0,0)
  BaseFeature = -> Pad643
  Profile = -> Sketch1224
  ReferenceAxis = -> Sketch1224 [V_Axis]
  Reversed = true
FEATURE [PartDesign::Chamfer] Chamfer234  label="M3 Nut Smooth Hole099"
  Base = -> Groove130 [Edge24,Edge23]
  BaseFeature = -> Groove130
  Size = 0.2
FEATURE [PartDesign::Groove] Groove132  label="M3 Nut Smooth126"
  Angle = 360
  Axis = (-2e-16,3e-16,1)
  Base = (0,0,0)
  BaseFeature = -> Pad566
  Profile = -> Sketch1203
  ReferenceAxis = -> Sketch1203 [V_Axis]
  Reversed = true
FEATURE [PartDesign::Pocket] Pocket558  label="M3x8 Wrench078"
  BaseFeature = -> Pad630
  Length = 1.3
  Length2 = 100
  Profile = -> Sketch1201
  Type = 0
FEATURE [PartDesign::Chamfer] Chamfer238  label="M3x8 Smooth061"
  Base = -> Pocket558 [Face11,Edge2,Edge24,Edge3]
  BaseFeature = -> Pocket558
  Size = 0.2
FEATURE [PartDesign::Pad] Pad644  label="Baseplate028"
  Length = 12
  Length2 = 100
  Profile = -> Sketch1242
  Type = 0
FEATURE [Sketcher::SketchObject] Sketch1251
  MapMode = 5
  Placement = pos=(0,0,12) rot=(0,0,1;0rad)
  Support = -> [Pad644]
  sketch-geometry (9):
    g0: Circle [constr] CenterX=0 CenterY=0 CenterZ=0 NormalX=0 NormalY=0 NormalZ=1 AngleXU=0 Radius=20
    g1: LineSegment [constr] StartX=-14.1421 StartY=14.1421 StartZ=0 EndX=14.1421 EndY=14.1421 EndZ=0
    g2: LineSegment [constr] StartX=14.1421 StartY=14.1421 StartZ=0 EndX=14.1421 EndY=-14.1421 EndZ=0
    g3: LineSegment [constr] StartX=14.1421 StartY=-14.1421 StartZ=0 EndX=-14.1421 EndY=-14.1421 EndZ=0
    g4: LineSegment [constr] StartX=-14.1421 StartY=-14.1421 StartZ=0 EndX=-14.1421 EndY=14.1421 EndZ=0
    g5: Circle CenterX=-14.1421 CenterY=14.1421 CenterZ=0 NormalX=0 NormalY=0 NormalZ=1 AngleXU=0 Radius=1.6
    g6: Circle CenterX=14.1421 CenterY=14.1421 CenterZ=0 NormalX=0 NormalY=0 NormalZ=1 AngleXU=0 Radius=1.6
    g7: Circle CenterX=14.1421 CenterY=-14.1421 CenterZ=0 NormalX=0 NormalY=0 NormalZ=1 AngleXU=0 Radius=1.6
    g8: Circle CenterX=-14.1421 CenterY=-14.1421 CenterZ=0 NormalX=0 NormalY=0 NormalZ=1 AngleXU=0 Radius=1.6
  constraints (22):
    c: Coincident(g0,g-1)
    c: Radius(g0) = 20
    c: Coincident(g1,g2)
    c: Coincident(g2,g3)
    c: Coincident(g3,g4)
    c: Coincident(g4,g1)
    c: Horizontal(g1)
    c: Horizontal(g3)
    c: Vertical(g2)
    c: Vertical(g4)
    c: PointOnObject(g1,g0)
    c: PointOnObject(g2,g0)
    c: PointOnObject(g1,g0)
    c: Equal(g1,g2)
    c: Coincident(g5,g1)
    c: Coincident(g6,g1)
    c: Coincident(g7,g2)
    c: Coincident(g8,g3)
    c: Equal(g8,g5)
    c: Equal(g5,g6)
    c: Equal(g6,g7)
    c: Radius(g6) = 1.6
FEATURE [PartDesign::Pocket] Pocket550  label="Screwholes Mounting002"
  BaseFeature = -> Pad644
  Length = 12
  Length2 = 100
  Profile = -> Sketch1251
  Type = 0
FEATURE [Sketcher::SketchObject] Sketch1263
  MapMode = 5
  Placement = pos=(0,0,12) rot=(0,0,1;0rad)
  Support = -> [Pocket550]
  sketch-geometry (1):
    g0: Circle CenterX=0 CenterY=0 CenterZ=0 NormalX=0 NormalY=0 NormalZ=1 AngleXU=0 Radius=16.5
  constraints (2):
    c: Coincident(g0,g-1)
    c: Radius(g0) = 16.5
FEATURE [PartDesign::Pad] Pad645  label="M3 Nut Primitive125"
  Length = 1.2
  Length2 = 1.2
  Profile = -> Sketch1223
  Type = 4
FEATURE [Sketcher::SketchObject] Sketch1215
  ExternalGeometry = -> [Pad645]
  MapMode = 5
  Placement = pos=(0,0,0) rot=(0.57735,0.57735,0.57735;2.0944rad)
  Support = -> [YZ_Plane437]
  sketch-geometry (6):
    g0: LineSegment StartX=-2.67543 StartY=1.2 StartZ=0 EndX=-3.67543 EndY=1.2 EndZ=0
    g1: LineSegment StartX=-3.67543 StartY=1.2 StartZ=0 EndX=-3.67543 EndY=-1.2 EndZ=0
    g2: LineSegment StartX=-3.67543 StartY=-1.2 StartZ=0 EndX=-2.67543 EndY=-1.2 EndZ=0
    g3: LineSegment StartX=-2.67543 StartY=-1.2 StartZ=0 EndX=-3.17543 EndY=-1 EndZ=0
    g4: LineSegment StartX=-3.17543 StartY=-1 StartZ=0 EndX=-3.17543 EndY=1 EndZ=0
    g5: LineSegment StartX=-3.17543 StartY=1 StartZ=0 EndX=-2.67543 EndY=1.2 EndZ=0
  constraints (15):
    c: Horizontal(g0)
    c: Coincident(g0,g1)
    c: Coincident(g1,g2)
    c: Coincident(g2,g3)
    c: Coincident(g3,g4)
    c: Coincident(g4,g5)
    c: Coincident(g5,g0)
    c: Symmetric(g4,g3,g-1)
    c: Symmetric(g0,g2,g-1)
    c: Symmetric(g1,g0,g-1)
    c: DistanceX(g0,g4) = 0.5
    c: DistanceY(g3,g4) = 2
    c: DistanceY(g1,g0) = 2.4
    c: PointOnObject(g3,g-3)
    c: DistanceX(g4,g0) = 0.5
FEATURE [PartDesign::Pocket] Pocket560  label="Accesshole002"
  BaseFeature = -> Pocket550
  Length = 7
  Length2 = 100
  Profile = -> Sketch1263
  Type = 0
FEATURE [PartDesign::Groove] Groove133  label="M3 Nut Smooth127"
  Angle = 360
  Axis = (-2e-16,3e-16,1)
  Base = (0,0,0)
  BaseFeature = -> Pad645
  Profile = -> Sketch1215
  ReferenceAxis = -> Sketch1215 [V_Axis]
  Reversed = true
FEATURE [PartDesign::Pad] Pad647  label="M3x20 Thread055"
  BaseFeature = -> Pad563
  Length = 20
  Length2 = 100
  Profile = -> Sketch1229
  Type = 0
FEATURE [Sketcher::SketchObject] Sketch1227
  MapMode = 5
  Placement = pos=(0,0,0) rot=(1,0,0;3.14159rad)
  Support = -> [Pad647]
  sketch-geometry (7):
    g0: LineSegment StartX=1.275 StartY=0.736122 StartZ=0 EndX=0 EndY=1.47224 EndZ=0
    g1: LineSegment StartX=0 StartY=1.47224 StartZ=0 EndX=-1.275 EndY=0.736122 EndZ=0
    g2: LineSegment StartX=-1.275 StartY=0.736122 StartZ=0 EndX=-1.275 EndY=-0.736122 EndZ=0
    g3: LineSegment StartX=-1.275 StartY=-0.736122 StartZ=0 EndX=1.34766e-11 EndY=-1.47224 EndZ=0
    g4: LineSegment StartX=1.34766e-11 StartY=-1.47224 StartZ=0 EndX=1.275 EndY=-0.736122 EndZ=0
    g5: LineSegment StartX=1.275 StartY=-0.736122 StartZ=0 EndX=1.275 EndY=0.736122 EndZ=0
    g6: Circle [constr] CenterX=0 CenterY=0 CenterZ=0 NormalX=0 NormalY=0 NormalZ=1 AngleXU=0 Radius=1.47224
  constraints (16):
    c: Coincident(g0,g1)
    c: Coincident(g1,g2)
    c: Coincident(g2,g3)
    c: Coincident(g3,g4)
    c: Coincident(g4,g5)
    c: Coincident(g5,g0)
    c: Equal(g0, g1-g5) x5
    c: PointOnObject(g0,g6)
    c: PointOnObject(g1,g6)
    c: PointOnObject(g2,g6)
    c: PointOnObject(g3,g6)
    c: PointOnObject(g4,g6)
    c: PointOnObject(g5,g6)
    c: Coincident(g6,g-1)
    c: PointOnObject(g0,g-2)
    c: DistanceX(g1,g0) = 2.55
FEATURE [PartDesign::Pocket] Pocket510  label="M3x20 Wrench045"
  BaseFeature = -> Pad647
  Length = 1.3
  Length2 = 100
  Profile = -> Sketch1227
  Type = 0
FEATURE [PartDesign::Chamfer] Chamfer236  label="M3x20 Smooth041"
  Base = -> Pocket510 [Face11,Edge2,Edge24,Edge3]
  BaseFeature = -> Pocket510
  Size = 0.2
FEATURE [PartDesign::Body] Body366  label="M3x077"
  Group = -> [Sketch1216,Pad563,Sketch1229,Pad647,Sketch1227,Pocket510,Chamfer236]
  Origin = -> Origin525
  Placement = pos=(11.25,-65.6,224.85) rot=(0,-1,0;1.5708rad)
  Tip = -> Chamfer236
FEATURE [PartDesign::Pad] Pad648
  Length = 5
  Length2 = 100
  Profile = -> Sketch1221
  Type = 0
FEATURE [Sketcher::SketchObject] Sketch1194
  ExternalGeometry = -> [Pad648]
  MapMode = 5
  Placement = pos=(0,0,5) rot=(0,0,1;0rad)
  Support = -> [Pad648]
  sketch-geometry (1):
    g0: Circle CenterX=0 CenterY=10.15 CenterZ=0 NormalX=0 NormalY=0 NormalZ=1 AngleXU=0 Radius=1.5
  constraints (2):
    c: Coincident(g0,g-3)
    c: Radius(g0) = 1.5
FEATURE [PartDesign::Pocket] Pocket559
  BaseFeature = -> Pad648
  Length = 4
  Length2 = 100
  Profile = -> Sketch1194
  Type = 0
FEATURE [PartDesign::Pad] Pad649
  BaseFeature = -> Pad575
  Length = 6
  Length2 = 100
  Profile = -> Sketch1195
  Type = 0
FEATURE [Sketcher::SketchObject] Sketch1202
  ExternalGeometry = -> [Pad649]
  MapMode = 5
  Placement = pos=(0,0,35.1) rot=(0,0,1;0rad)
  Support = -> [Pad649]
  sketch-geometry (7):
    g0: ArcOfCircle CenterX=-3e-16 CenterY=10.15 CenterZ=0 NormalX=0 NormalY=0 NormalZ=1 AngleXU=0 Radius=9.5 StartAngle=5.9573 EndAngle=9.75066
    g1: LineSegment StartX=-9 StartY=7.10862 StartZ=0 EndX=-9 EndY=-14.15 EndZ=0
    g2: LineSegment StartX=-9 StartY=-14.15 StartZ=0 EndX=-5 EndY=-14.15 EndZ=0
    g3: LineSegment StartX=5 StartY=-14.15 StartZ=0 EndX=9 EndY=-14.15 EndZ=0
    g4: LineSegment StartX=9 StartY=-14.15 StartZ=0 EndX=9 EndY=7.10862 EndZ=0
    g5: ArcOfCircle CenterX=-3e-16 CenterY=-10.4 CenterZ=0 NormalX=0 NormalY=0 NormalZ=1 AngleXU=0 Radius=6.25 StartAngle=3.78509 EndAngle=5.63968
    g6: LineSegment [constr] StartX=0 StartY=-20.15 StartZ=0 EndX=0 EndY=-16.65 EndZ=0
  constraints (22):
    c: Symmetric(g0,g0,g-2)
    c: Coincident(g1,g0)
    c: Vertical(g1)
    c: Coincident(g2,g1)
    c: Horizontal(g2)
    c: Horizontal(g3)
    c: Coincident(g4,g3)
    c: Coincident(g4,g0)
    c: Vertical(g4)
    c: Symmetric(g2,g3,g-2)
    c: Coincident(g5,g2)
    c: Coincident(g5,g3)
    c: DistanceY(g-3,g3) = 6
    c: DistanceY(g0,g-4) = 10
    c: Radius(g0) = 9.5
    c: DistanceX(g0,g0) = 18
    c: PointOnObject(g6,g-3)
    c: PointOnObject(g6,g5)
    c: Vertical(g6)
    c: DistanceY(g6,g6) = 3.5
    c: DistanceX(g2,g3) = 10
    c: PointOnObject(g6,g-2)
FEATURE [PartDesign::Pad] Pad640
  BaseFeature = -> Pad649
  Length = 2.5
  Length2 = 100
  Profile = -> Sketch1202
  Type = 0
FEATURE [Sketcher::SketchObject] Sketch1206
  ExternalGeometry = -> [Pad640]
  MapMode = 5
  Placement = pos=(0,0,37.6) rot=(0,0,1;0rad)
  Support = -> [Pad640]
  sketch-geometry (1):
    g0: Circle CenterX=-3e-16 CenterY=10.15 CenterZ=0 NormalX=0 NormalY=0 NormalZ=1 AngleXU=0 Radius=6.5
  constraints (2):
    c: Coincident(g0,g-3)
    c: Radius(g0) = 6.5
FEATURE [PartDesign::Pad] Pad548
  BaseFeature = -> Pad640
  Length = 1
  Length2 = 100
  Profile = -> Sketch1206
  Type = 0
FEATURE [Sketcher::SketchObject] Sketch1188
  ExternalGeometry = -> [Pad548]
  MapMode = 5
  Placement = pos=(0,0,38.6) rot=(0,0,1;0rad)
  Support = -> [Pad548]
  sketch-geometry (1):
    g0: Circle CenterX=0 CenterY=10.15 CenterZ=0 NormalX=0 NormalY=0 NormalZ=1 AngleXU=0 Radius=5.5
  constraints (2):
    c: Coincident(g0,g-3)
    c: Radius(g0) = 5.5
FEATURE [PartDesign::Pad] Pad565
  BaseFeature = -> Pad548
  Length = 0.5
  Length2 = 100
  Profile = -> Sketch1188
  Type = 0
FEATURE [Sketcher::SketchObject] Sketch1207
  ExternalGeometry = -> [Pad565]
  MapMode = 5
  Placement = pos=(0,0,39.1) rot=(0,0,1;0rad)
  Support = -> [Pad565]
  sketch-geometry (1):
    g0: Circle CenterX=0 CenterY=10.15 CenterZ=0 NormalX=0 NormalY=0 NormalZ=1 AngleXU=0 Radius=3
  constraints (2):
    c: Coincident(g0,g-3)
    c: Radius(g0) = 3
FEATURE [PartDesign::Pad] Pad560
  BaseFeature = -> Pad565
  Length = 4
  Length2 = 100
  Profile = -> Sketch1207
  Type = 0
FEATURE [Sketcher::SketchObject] Sketch1212
  ExternalGeometry = -> [Pad560]
  MapMode = 5
  Placement = pos=(0,0,43.1) rot=(0,0,1;0rad)
  Support = -> [Pad560]
  sketch-geometry (1):
    g0: Circle CenterX=0 CenterY=10.15 CenterZ=0 NormalX=0 NormalY=0 NormalZ=1 AngleXU=0 Radius=1.5
  constraints (2):
    c: Coincident(g0,g-3)
    c: Radius(g0) = 1.5
FEATURE [PartDesign::Pocket] Pocket556
  BaseFeature = -> Pad560
  Length = 5
  Length2 = 100
  Profile = -> Sketch1212
  Type = 0
FEATURE [Sketcher::SketchObject] Sketch1177
  MapMode = 5
  Placement = pos=(0,0,29.1) rot=(0,0,1;0rad)
  Support = -> [Pocket556]
  sketch-geometry (4):
    g0: Circle CenterX=-4.91157 CenterY=25.3 CenterZ=0 NormalX=0 NormalY=0 NormalZ=1 AngleXU=0 Radius=2.25
    g1: Circle CenterX=4.91157 CenterY=25.3 CenterZ=0 NormalX=0 NormalY=0 NormalZ=1 AngleXU=0 Radius=2.25
    g2: Circle CenterX=-4.91157 CenterY=-25.3 CenterZ=0 NormalX=0 NormalY=0 NormalZ=1 AngleXU=0 Radius=2.25
    g3: Circle CenterX=4.91157 CenterY=-25.3 CenterZ=0 NormalX=0 NormalY=0 NormalZ=1 AngleXU=0 Radius=2.25
  constraints (8):
    c: Equal(g3,g2)
    c: Equal(g2,g1)
    c: Equal(g1,g0)
    c: Radius(g1) = 2.25
    c: Symmetric(g1,g0,g-2)
    c: Symmetric(g3,g2,g-2)
    c: Symmetric(g3,g1,g-1)
    c: DistanceY(g3,g1) = 50.6
FEATURE [PartDesign::Pad] Pad650  label="M3 Nut Primitive126"
  Length = 1.2
  Length2 = 1.2
  Profile = -> Sketch1174
  Type = 4
FEATURE [Sketcher::SketchObject] Sketch1176
  ExternalGeometry = -> [Pad650]
  MapMode = 5
  Placement = pos=(0,0,0) rot=(0.57735,0.57735,0.57735;2.0944rad)
  Support = -> [YZ_Plane430]
  sketch-geometry (6):
    g0: LineSegment StartX=-2.67543 StartY=1.2 StartZ=0 EndX=-3.67543 EndY=1.2 EndZ=0
    g1: LineSegment StartX=-3.67543 StartY=1.2 StartZ=0 EndX=-3.67543 EndY=-1.2 EndZ=0
    g2: LineSegment StartX=-3.67543 StartY=-1.2 StartZ=0 EndX=-2.67543 EndY=-1.2 EndZ=0
    g3: LineSegment StartX=-2.67543 StartY=-1.2 StartZ=0 EndX=-3.17543 EndY=-1 EndZ=0
    g4: LineSegment StartX=-3.17543 StartY=-1 StartZ=0 EndX=-3.17543 EndY=1 EndZ=0
    g5: LineSegment StartX=-3.17543 StartY=1 StartZ=0 EndX=-2.67543 EndY=1.2 EndZ=0
  constraints (15):
    c: Horizontal(g0)
    c: Coincident(g0,g1)
    c: Coincident(g1,g2)
    c: Coincident(g2,g3)
    c: Coincident(g3,g4)
    c: Coincident(g4,g5)
    c: Coincident(g5,g0)
    c: Symmetric(g4,g3,g-1)
    c: Symmetric(g0,g2,g-1)
    c: Symmetric(g1,g0,g-1)
    c: DistanceX(g0,g4) = 0.5
    c: DistanceY(g3,g4) = 2
    c: DistanceY(g1,g0) = 2.4
    c: PointOnObject(g3,g-3)
    c: DistanceX(g4,g0) = 0.5
FEATURE [PartDesign::Groove] Groove128  label="M3 Nut Smooth122"
  Angle = 360
  Axis = (-2e-16,3e-16,1)
  Base = (0,0,0)
  BaseFeature = -> Pad650
  Profile = -> Sketch1176
  ReferenceAxis = -> Sketch1176 [V_Axis]
  Reversed = true
FEATURE [PartDesign::Chamfer] Chamfer232  label="M3 Nut Smooth Hole098"
  Base = -> Groove128 [Edge24,Edge23]
  BaseFeature = -> Groove128
  Size = 0.2
FEATURE [PartDesign::Pocket] Pocket564
  BaseFeature = -> Pocket556
  Length = 5
  Length2 = 100
  Profile = -> Sketch1177
  Type = 0
FEATURE [Sketcher::SketchObject] Sketch1225
  MapMode = 5
  Placement = pos=(0,0,29.1) rot=(0,0,1;0rad)
  Support = -> [Pocket564]
  sketch-geometry (8):
    g0: LineSegment StartX=-0.5 StartY=26.8 StartZ=0 EndX=0.5 EndY=26.8 EndZ=0
    g1: LineSegment StartX=0.5 StartY=26.8 StartZ=0 EndX=0.5 EndY=20.15 EndZ=0
    g2: LineSegment StartX=0.5 StartY=20.15 StartZ=0 EndX=-0.5 EndY=20.15 EndZ=0
    g3: LineSegment StartX=-0.5 StartY=20.15 StartZ=0 EndX=-0.5 EndY=26.8 EndZ=0
    g4: LineSegment StartX=-0.5 StartY=-20.15 StartZ=0 EndX=0.5 EndY=-20.15 EndZ=0
    g5: LineSegment StartX=0.5 StartY=-20.15 StartZ=0 EndX=0.5 EndY=-26.8 EndZ=0
    g6: LineSegment StartX=0.5 StartY=-26.8 StartZ=0 EndX=-0.5 EndY=-26.8 EndZ=0
    g7: LineSegment StartX=-0.5 StartY=-26.8 StartZ=0 EndX=-0.5 EndY=-20.15 EndZ=0
  constraints (20):
    c: Coincident(g0,g1)
    c: Coincident(g1,g2)
    c: Coincident(g2,g3)
    c: Coincident(g3,g0)
    c: Horizontal(g2)
    c: Vertical(g1)
    c: Vertical(g3)
    c: Coincident(g4,g5)
    c: Coincident(g5,g6)
    c: Coincident(g6,g7)
    c: Coincident(g7,g4)
    c: Horizontal(g6)
    c: Vertical(g7)
    c: Symmetric(g4,g4,g-2)
    c: Symmetric(g0,g0,g-2)
    c: Symmetric(g0,g5,g-1)
    c: DistanceY(g5,g0) = 53.6
    c: DistanceY(g4,g1) = 40.3
    c: DistanceX(g0,g0) = 1
    c: Symmetric(g4,g1,g-1)
FEATURE [PartDesign::Pad] Pad646
  BaseFeature = -> Pocket564
  Length = 2
  Length2 = 100
  Profile = -> Sketch1225
  Type = 0
FEATURE [Sketcher::SketchObject] Sketch1265
  ExternalGeometry = -> [Pad646]
  MapMode = 5
  Placement = pos=(0.5,0,0) rot=(0.57735,0.57735,0.57735;2.0944rad)
  Support = -> [Pad646]
  sketch-geometry (6):
    g0: LineSegment StartX=-26.8 StartY=29.1 StartZ=0 EndX=-26.8 EndY=31.1 EndZ=0
    g1: LineSegment StartX=-26.8 StartY=31.1 StartZ=0 EndX=-20.15 EndY=31.1 EndZ=0
    g2: LineSegment StartX=-20.15 StartY=31.1 StartZ=0 EndX=-26.8 EndY=29.1 EndZ=0
    g3: LineSegment StartX=20.15 StartY=31.1 StartZ=0 EndX=26.8 EndY=31.1 EndZ=0
    g4: LineSegment StartX=26.8 StartY=31.1 StartZ=0 EndX=26.8 EndY=29.1 EndZ=0
    g5: LineSegment StartX=26.8 StartY=29.1 StartZ=0 EndX=20.15 EndY=31.1 EndZ=0
  constraints (14):
    c: Vertical(g0)
    c: Coincident(g0,g1)
    c: Horizontal(g1)
    c: Coincident(g1,g2)
    c: Coincident(g2,g0)
    c: Coincident(g3,g4)
    c: Coincident(g4,g5)
    c: Coincident(g5,g3)
    c: Symmetric(g0,g4,g-2)
    c: Symmetric(g3,g0,g-2)
    c: Symmetric(g1,g3,g-2)
    c: DistanceX(g0,g3) = 53.6
    c: DistanceY(g4,g4) = 2
    c: Coincident(g3,g-3)
FEATURE [PartDesign::Pocket] Pocket557
  BaseFeature = -> Pad646
  Length = 1
  Length2 = 100
  Profile = -> Sketch1265
  Type = 0
FEATURE [Sketcher::SketchObject] Sketch1375
  MapMode = 5
  Support = -> [XY_Plane497]
  sketch-geometry (8):
    g0: LineSegment StartX=0 StartY=3.17543 StartZ=0 EndX=-2.75 EndY=1.58771 EndZ=0
    g1: LineSegment StartX=-2.75 StartY=1.58771 StartZ=0 EndX=-2.75 EndY=-1.58771 EndZ=0
    g2: LineSegment StartX=-2.75 StartY=-1.58771 StartZ=0 EndX=0 EndY=-3.17543 EndZ=0
    g3: LineSegment StartX=0 StartY=-3.17543 StartZ=0 EndX=2.75 EndY=-1.58771 EndZ=0
    g4: LineSegment StartX=2.75 StartY=-1.58771 StartZ=0 EndX=2.75 EndY=1.58771 EndZ=0
    g5: LineSegment StartX=2.75 StartY=1.58771 StartZ=0 EndX=0 EndY=3.17543 EndZ=0
    g6: Circle [constr] CenterX=0 CenterY=0 CenterZ=0 NormalX=0 NormalY=0 NormalZ=1 AngleXU=0 Radius=3.17543
    g7: Circle CenterX=0 CenterY=0 CenterZ=0 NormalX=0 NormalY=0 NormalZ=1 AngleXU=0 Radius=1.5
  constraints (18):
    c: Coincident(g0,g1)
    c: Coincident(g1,g2)
    c: Coincident(g2,g3)
    c: Coincident(g3,g4)
    c: Coincident(g4,g5)
    c: Coincident(g5,g0)
    c: Equal(g0, g1-g5) x5
    c: PointOnObject(g0,g6)
    c: PointOnObject(g1,g6)
    c: PointOnObject(g2,g6)
    c: PointOnObject(g3,g6)
    c: PointOnObject(g4,g6)
    c: PointOnObject(g5,g6)
    c: Coincident(g6,g-1)
    c: PointOnObject(g5,g-2)
    c: DistanceX(g0,g4) = 5.5
    c: Coincident(g7,g-1)
    c: Radius(g7) = 1.5
FEATURE [PartDesign::Pad] Pad586  label="M3 Nut Primitive113"
  Length = 1.2
  Length2 = 1.2
  Profile = -> Sketch1375
  Type = 4
FEATURE [Sketcher::SketchObject] Sketch1376
  MapMode = 5
  Support = -> [XY_Plane509]
  sketch-geometry (8):
    g0: LineSegment StartX=0 StartY=3.17543 StartZ=0 EndX=-2.75 EndY=1.58771 EndZ=0
    g1: LineSegment StartX=-2.75 StartY=1.58771 StartZ=0 EndX=-2.75 EndY=-1.58771 EndZ=0
    g2: LineSegment StartX=-2.75 StartY=-1.58771 StartZ=0 EndX=0 EndY=-3.17543 EndZ=0
    g3: LineSegment StartX=0 StartY=-3.17543 StartZ=0 EndX=2.75 EndY=-1.58771 EndZ=0
    g4: LineSegment StartX=2.75 StartY=-1.58771 StartZ=0 EndX=2.75 EndY=1.58771 EndZ=0
    g5: LineSegment StartX=2.75 StartY=1.58771 StartZ=0 EndX=0 EndY=3.17543 EndZ=0
    g6: Circle [constr] CenterX=0 CenterY=0 CenterZ=0 NormalX=0 NormalY=0 NormalZ=1 AngleXU=0 Radius=3.17543
    g7: Circle CenterX=0 CenterY=0 CenterZ=0 NormalX=0 NormalY=0 NormalZ=1 AngleXU=0 Radius=1.5
  constraints (18):
    c: Coincident(g0,g1)
    c: Coincident(g1,g2)
    c: Coincident(g2,g3)
    c: Coincident(g3,g4)
    c: Coincident(g4,g5)
    c: Coincident(g5,g0)
    c: Equal(g0, g1-g5) x5
    c: PointOnObject(g0,g6)
    c: PointOnObject(g1,g6)
    c: PointOnObject(g2,g6)
    c: PointOnObject(g3,g6)
    c: PointOnObject(g4,g6)
    c: PointOnObject(g5,g6)
    c: Coincident(g6,g-1)
    c: PointOnObject(g5,g-2)
    c: DistanceX(g0,g4) = 5.5
    c: Coincident(g7,g-1)
    c: Radius(g7) = 1.5
FEATURE [PartDesign::Pad] Pad498  label="M3 Nut Primitive096"
  Length = 1.2
  Length2 = 1.2
  Profile = -> Sketch1376
  Type = 4
FEATURE [Sketcher::SketchObject] Sketch1370
  ExternalGeometry = -> [Pad498]
  MapMode = 5
  Placement = pos=(0,0,0) rot=(0.57735,0.57735,0.57735;2.0944rad)
  Support = -> [YZ_Plane492]
  sketch-geometry (6):
    g0: LineSegment StartX=-2.67543 StartY=1.2 StartZ=0 EndX=-3.67543 EndY=1.2 EndZ=0
    g1: LineSegment StartX=-3.67543 StartY=1.2 StartZ=0 EndX=-3.67543 EndY=-1.2 EndZ=0
    g2: LineSegment StartX=-3.67543 StartY=-1.2 StartZ=0 EndX=-2.67543 EndY=-1.2 EndZ=0
    g3: LineSegment StartX=-2.67543 StartY=-1.2 StartZ=0 EndX=-3.17543 EndY=-1 EndZ=0
    g4: LineSegment StartX=-3.17543 StartY=-1 StartZ=0 EndX=-3.17543 EndY=1 EndZ=0
    g5: LineSegment StartX=-3.17543 StartY=1 StartZ=0 EndX=-2.67543 EndY=1.2 EndZ=0
  constraints (15):
    c: Horizontal(g0)
    c: Coincident(g0,g1)
    c: Coincident(g1,g2)
    c: Coincident(g2,g3)
    c: Coincident(g3,g4)
    c: Coincident(g4,g5)
    c: Coincident(g5,g0)
    c: Symmetric(g4,g3,g-1)
    c: Symmetric(g0,g2,g-1)
    c: Symmetric(g1,g0,g-1)
    c: DistanceX(g0,g4) = 0.5
    c: DistanceY(g3,g4) = 2
    c: DistanceY(g1,g0) = 2.4
    c: PointOnObject(g3,g-3)
    c: DistanceX(g4,g0) = 0.5
FEATURE [PartDesign::Groove] Groove119  label="M3 Nut Smooth113"
  Angle = 360
  Axis = (-2e-16,3e-16,1)
  Base = (0,0,0)
  BaseFeature = -> Pad498
  Profile = -> Sketch1370
  ReferenceAxis = -> Sketch1370 [V_Axis]
  Reversed = true
FEATURE [PartDesign::Chamfer] Chamfer219  label="M3 Nut Smooth Hole092"
  Base = -> Groove119 [Edge24,Edge23]
  BaseFeature = -> Groove119
  Size = 0.2
FEATURE [PartDesign::Body] Body338  label="M3 Nut061"
  Group = -> [Sketch1376,Pad498,Sketch1370,Groove119,Chamfer219]
  Origin = -> Origin489
  Placement = pos=(-71.5,-9.8,62.05) rot=(0.57735,-0.57735,0.57735;2.0944rad)
  Tip = -> Chamfer219
FEATURE [Sketcher::SketchObject] Sketch1378
  ExternalGeometry = -> [Pad586]
  MapMode = 5
  Placement = pos=(0,0,0) rot=(0.57735,0.57735,0.57735;2.0944rad)
  Support = -> [YZ_Plane495]
  sketch-geometry (6):
    g0: LineSegment StartX=-2.67543 StartY=1.2 StartZ=0 EndX=-3.67543 EndY=1.2 EndZ=0
    g1: LineSegment StartX=-3.67543 StartY=1.2 StartZ=0 EndX=-3.67543 EndY=-1.2 EndZ=0
    g2: LineSegment StartX=-3.67543 StartY=-1.2 StartZ=0 EndX=-2.67543 EndY=-1.2 EndZ=0
    g3: LineSegment StartX=-2.67543 StartY=-1.2 StartZ=0 EndX=-3.17543 EndY=-1 EndZ=0
    g4: LineSegment StartX=-3.17543 StartY=-1 StartZ=0 EndX=-3.17543 EndY=1 EndZ=0
    g5: LineSegment StartX=-3.17543 StartY=1 StartZ=0 EndX=-2.67543 EndY=1.2 EndZ=0
  constraints (15):
    c: Horizontal(g0)
    c: Coincident(g0,g1)
    c: Coincident(g1,g2)
    c: Coincident(g2,g3)
    c: Coincident(g3,g4)
    c: Coincident(g4,g5)
    c: Coincident(g5,g0)
    c: Symmetric(g4,g3,g-1)
    c: Symmetric(g0,g2,g-1)
    c: Symmetric(g1,g0,g-1)
    c: DistanceX(g0,g4) = 0.5
    c: DistanceY(g3,g4) = 2
    c: DistanceY(g1,g0) = 2.4
    c: PointOnObject(g3,g-3)
    c: DistanceX(g4,g0) = 0.5
FEATURE [PartDesign::Groove] Groove118  label="M3 Nut Smooth112"
  Angle = 360
  Axis = (-2e-16,3e-16,1)
  Base = (0,0,0)
  BaseFeature = -> Pad586
  Profile = -> Sketch1378
  ReferenceAxis = -> Sketch1378 [V_Axis]
  Reversed = true
FEATURE [PartDesign::Chamfer] Chamfer254  label="M3 Nut Smooth Hole107"
  Base = -> Groove118 [Edge24,Edge23]
  BaseFeature = -> Groove118
  Size = 0.2
FEATURE [Sketcher::SketchObject] Sketch1382
  MapMode = 5
  Placement = pos=(0,0,0) rot=(1,0,0;1.5708rad)
  Support = -> [XZ_Plane511]
  sketch-geometry (1):
    g0: Circle CenterX=1.55 CenterY=4 CenterZ=0 NormalX=0 NormalY=0 NormalZ=1 AngleXU=0 Radius=0.75
  constraints (3):
    c: Radius(g0) = 0.75
    c: DistanceY(g-1,g0) = 4
    c: DistanceX(g-1,g0) = 1.55
FEATURE [PartDesign::Pad] Pad490
  Length = 10
  Length2 = 100
  Placement = pos=(0,0,0) rot=(1,0,0;1.5708rad)
  Profile = -> Sketch1382
  Reversed = true
  Type = 0
FEATURE [PartDesign::Body] Body314  label="brown wire009"
  Group = -> [Sketch1382,Pad490]
  Origin = -> Origin465
  Placement = pos=(0,25.15,0) rot=(0,0,1;0rad)
  Tip = -> Pad490
FEATURE [Sketcher::SketchObject] Sketch1384
  MapMode = 5
  Support = -> [XY_Plane499]
  sketch-geometry (8):
    g0: LineSegment StartX=0 StartY=3.17543 StartZ=0 EndX=-2.75 EndY=1.58771 EndZ=0
    g1: LineSegment StartX=-2.75 StartY=1.58771 StartZ=0 EndX=-2.75 EndY=-1.58771 EndZ=0
    g2: LineSegment StartX=-2.75 StartY=-1.58771 StartZ=0 EndX=0 EndY=-3.17543 EndZ=0
    g3: LineSegment StartX=0 StartY=-3.17543 StartZ=0 EndX=2.75 EndY=-1.58771 EndZ=0
    g4: LineSegment StartX=2.75 StartY=-1.58771 StartZ=0 EndX=2.75 EndY=1.58771 EndZ=0
    g5: LineSegment StartX=2.75 StartY=1.58771 StartZ=0 EndX=0 EndY=3.17543 EndZ=0
    g6: Circle [constr] CenterX=0 CenterY=0 CenterZ=0 NormalX=0 NormalY=0 NormalZ=1 AngleXU=0 Radius=3.17543
    g7: Circle CenterX=0 CenterY=0 CenterZ=0 NormalX=0 NormalY=0 NormalZ=1 AngleXU=0 Radius=1.5
  constraints (18):
    c: Coincident(g0,g1)
    c: Coincident(g1,g2)
    c: Coincident(g2,g3)
    c: Coincident(g3,g4)
    c: Coincident(g4,g5)
    c: Coincident(g5,g0)
    c: Equal(g0, g1-g5) x5
    c: PointOnObject(g0,g6)
    c: PointOnObject(g1,g6)
    c: PointOnObject(g2,g6)
    c: PointOnObject(g3,g6)
    c: PointOnObject(g4,g6)
    c: PointOnObject(g5,g6)
    c: Coincident(g6,g-1)
    c: PointOnObject(g5,g-2)
    c: DistanceX(g0,g4) = 5.5
    c: Coincident(g7,g-1)
    c: Radius(g7) = 1.5
FEATURE [PartDesign::Pad] Pad499  label="M3 Nut Primitive097"
  Length = 1.2
  Length2 = 1.2
  Profile = -> Sketch1384
  Type = 4
FEATURE [Sketcher::SketchObject] Sketch1379
  ExternalGeometry = -> [Pad499]
  MapMode = 5
  Placement = pos=(0,0,0) rot=(0.57735,0.57735,0.57735;2.0944rad)
  Support = -> [YZ_Plane499]
  sketch-geometry (6):
    g0: LineSegment StartX=-2.67543 StartY=1.2 StartZ=0 EndX=-3.67543 EndY=1.2 EndZ=0
    g1: LineSegment StartX=-3.67543 StartY=1.2 StartZ=0 EndX=-3.67543 EndY=-1.2 EndZ=0
    g2: LineSegment StartX=-3.67543 StartY=-1.2 StartZ=0 EndX=-2.67543 EndY=-1.2 EndZ=0
    g3: LineSegment StartX=-2.67543 StartY=-1.2 StartZ=0 EndX=-3.17543 EndY=-1 EndZ=0
    g4: LineSegment StartX=-3.17543 StartY=-1 StartZ=0 EndX=-3.17543 EndY=1 EndZ=0
    g5: LineSegment StartX=-3.17543 StartY=1 StartZ=0 EndX=-2.67543 EndY=1.2 EndZ=0
  constraints (15):
    c: Horizontal(g0)
    c: Coincident(g0,g1)
    c: Coincident(g1,g2)
    c: Coincident(g2,g3)
    c: Coincident(g3,g4)
    c: Coincident(g4,g5)
    c: Coincident(g5,g0)
    c: Symmetric(g4,g3,g-1)
    c: Symmetric(g0,g2,g-1)
    c: Symmetric(g1,g0,g-1)
    c: DistanceX(g0,g4) = 0.5
    c: DistanceY(g3,g4) = 2
    c: DistanceY(g1,g0) = 2.4
    c: PointOnObject(g3,g-3)
    c: DistanceX(g4,g0) = 0.5
FEATURE [PartDesign::Groove] Groove117  label="M3 Nut Smooth111"
  Angle = 360
  Axis = (-2e-16,3e-16,1)
  Base = (0,0,0)
  BaseFeature = -> Pad499
  Profile = -> Sketch1379
  ReferenceAxis = -> Sketch1379 [V_Axis]
  Reversed = true
FEATURE [PartDesign::Chamfer] Chamfer246  label="M3 Nut Smooth Hole103"
  Base = -> Groove117 [Edge24,Edge23]
  BaseFeature = -> Groove117
  Size = 0.2
FEATURE [PartDesign::Body] Body336  label="M3 Nut059"
  Group = -> [Sketch1384,Pad499,Sketch1379,Groove117,Chamfer246]
  Origin = -> Origin503
  Placement = pos=(-23,-9.8,62.05) rot=(0.57735,-0.57735,0.57735;2.0944rad)
  Tip = -> Chamfer246
FEATURE [Sketcher::SketchObject] Sketch1387
  MapMode = 5
  Support = -> [XY_Plane513]
  sketch-geometry (4):
    g0: LineSegment StartX=-10 StartY=20.15 StartZ=0 EndX=10 EndY=20.15 EndZ=0
    g1: LineSegment StartX=10 StartY=20.15 StartZ=0 EndX=10 EndY=-20.15 EndZ=0
    g2: LineSegment StartX=10 StartY=-20.15 StartZ=0 EndX=-10 EndY=-20.15 EndZ=0
    g3: LineSegment StartX=-10 StartY=-20.15 StartZ=0 EndX=-10 EndY=20.15 EndZ=0
  constraints (10):
    c: Coincident(g0,g1)
    c: Coincident(g1,g2)
    c: Coincident(g2,g3)
    c: Coincident(g3,g0)
    c: Horizontal(g2)
    c: Vertical(g3)
    c: DistanceX(g0,g0) = 20
    c: DistanceY(g1,g1) = 40.3
    c: Symmetric(g0,g1,g-1)
    c: Symmetric(g0,g0,g-2)
FEATURE [PartDesign::Pad] Pad493  label="Baseblock010"
  Length = 26.6
  Length2 = 100
  Profile = -> Sketch1387
  Type = 0
FEATURE [Sketcher::SketchObject] Sketch1389
  MapMode = 5
  Support = -> [XY_Plane528]
  sketch-geometry (1):
    g0: Circle CenterX=0 CenterY=10.15 CenterZ=0 NormalX=0 NormalY=0 NormalZ=1 AngleXU=0 Radius=3
  constraints (3):
    c: PointOnObject(g0,g-2)
    c: DistanceY(g-1,g0) = 10.15
    c: Radius(g0) = 3
FEATURE [PartDesign::Pad] Pad572
  Length = 5
  Length2 = 100
  Profile = -> Sketch1389
  Type = 0
FEATURE [Sketcher::SketchObject] Sketch1390
  ExternalGeometry = -> [Pad572]
  MapMode = 5
  Placement = pos=(0,0,5) rot=(0,0,1;0rad)
  Support = -> [Pad572]
  sketch-geometry (1):
    g0: Circle CenterX=0 CenterY=10.15 CenterZ=0 NormalX=0 NormalY=0 NormalZ=1 AngleXU=0 Radius=1.5
  constraints (2):
    c: Coincident(g0,g-3)
    c: Radius(g0) = 1.5
FEATURE [PartDesign::Pocket] Pocket523
  BaseFeature = -> Pad572
  Length = 4
  Length2 = 100
  Profile = -> Sketch1390
  Type = 0
FEATURE [PartDesign::Chamfer] Chamfer247
  Base = -> Pocket523 [Edge3]
  BaseFeature = -> Pocket523
  Size = 0.25
FEATURE [PartDesign::Body] Body332  label="Gear010"
  Group = -> [Sketch1389,Pad572,Sketch1390,Pocket523,Chamfer247]
  Origin = -> Origin534
  Placement = pos=(0,0,38.25) rot=(0,0,1;0rad)
  Tip = -> Chamfer247
FEATURE [Sketcher::SketchObject] Sketch1392
  MapMode = 5
  Support = -> [XY_Plane541]
  sketch-geometry (1):
    g0: Circle CenterX=0 CenterY=0 CenterZ=0 NormalX=0 NormalY=0 NormalZ=1 AngleXU=0 Radius=2.75
  constraints (2):
    c: Coincident(g0,g-1)
    c: Radius(g0) = 2.75
FEATURE [PartDesign::Pad] Pad583  label="M3x20 Head050"
  Length = 3
  Length2 = 100
  Profile = -> Sketch1392
  Type = 0
FEATURE [Sketcher::SketchObject] Sketch1393
  MapMode = 5
  Support = -> [XY_Plane502]
  sketch-geometry (8):
    g0: LineSegment StartX=0 StartY=3.17543 StartZ=0 EndX=-2.75 EndY=1.58771 EndZ=0
    g1: LineSegment StartX=-2.75 StartY=1.58771 StartZ=0 EndX=-2.75 EndY=-1.58771 EndZ=0
    g2: LineSegment StartX=-2.75 StartY=-1.58771 StartZ=0 EndX=0 EndY=-3.17543 EndZ=0
    g3: LineSegment StartX=0 StartY=-3.17543 StartZ=0 EndX=2.75 EndY=-1.58771 EndZ=0
    g4: LineSegment StartX=2.75 StartY=-1.58771 StartZ=0 EndX=2.75 EndY=1.58771 EndZ=0
    g5: LineSegment StartX=2.75 StartY=1.58771 StartZ=0 EndX=0 EndY=3.17543 EndZ=0
    g6: Circle [constr] CenterX=0 CenterY=0 CenterZ=0 NormalX=0 NormalY=0 NormalZ=1 AngleXU=0 Radius=3.17543
    g7: Circle CenterX=0 CenterY=0 CenterZ=0 NormalX=0 NormalY=0 NormalZ=1 AngleXU=0 Radius=1.5
  constraints (18):
    c: Coincident(g0,g1)
    c: Coincident(g1,g2)
    c: Coincident(g2,g3)
    c: Coincident(g3,g4)
    c: Coincident(g4,g5)
    c: Coincident(g5,g0)
    c: Equal(g0, g1-g5) x5
    c: PointOnObject(g0,g6)
    c: PointOnObject(g1,g6)
    c: PointOnObject(g2,g6)
    c: PointOnObject(g3,g6)
    c: PointOnObject(g4,g6)
    c: PointOnObject(g5,g6)
    c: Coincident(g6,g-1)
    c: PointOnObject(g5,g-2)
    c: DistanceX(g0,g4) = 5.5
    c: Coincident(g7,g-1)
    c: Radius(g7) = 1.5
FEATURE [Sketcher::SketchObject] Sketch1395
  MapMode = 5
  Placement = pos=(0,0,0) rot=(1,0,0;1.5708rad)
  Support = -> [XZ_Plane530]
  sketch-geometry (1):
    g0: Circle CenterX=-1.55 CenterY=4 CenterZ=0 NormalX=0 NormalY=0 NormalZ=1 AngleXU=0 Radius=0.75
  constraints (3):
    c: Radius(g0) = 0.75
    c: DistanceY(g-1,g0) = 4
    c: DistanceX(g0,g-1) = 1.55
FEATURE [PartDesign::Pad] Pad584
  Length = 10
  Length2 = 100
  Placement = pos=(0,0,0) rot=(1,0,0;1.5708rad)
  Profile = -> Sketch1395
  Reversed = true
  Type = 0
FEATURE [PartDesign::Body] Body343  label="orange wire009"
  Group = -> [Sketch1395,Pad584]
  Origin = -> Origin424
  Placement = pos=(0,25.15,0) rot=(0,0,1;0rad)
  Tip = -> Pad584
FEATURE [Sketcher::SketchObject] Sketch1400
  MapMode = 5
  Support = -> [XY_Plane527]
  sketch-geometry (1):
    g0: Circle CenterX=0 CenterY=0 CenterZ=0 NormalX=0 NormalY=0 NormalZ=1 AngleXU=0 Radius=2.75
  constraints (2):
    c: Coincident(g0,g-1)
    c: Radius(g0) = 2.75
FEATURE [PartDesign::Pad] Pad573  label="M3x20 Head049"
  Length = 3
  Length2 = 100
  Profile = -> Sketch1400
  Type = 0
FEATURE [Sketcher::SketchObject] Sketch1401
  MapMode = 5
  Placement = pos=(0,0,0) rot=(1,0,0;1.5708rad)
  Support = -> [XZ_Plane523]
  sketch-geometry (1):
    g0: Circle CenterX=0 CenterY=4 CenterZ=0 NormalX=0 NormalY=0 NormalZ=1 AngleXU=0 Radius=0.75
  constraints (3):
    c: PointOnObject(g0,g-2)
    c: Radius(g0) = 0.75
    c: DistanceY(g-1,g0) = 4
FEATURE [PartDesign::Pad] Pad569
  Length = 10
  Length2 = 100
  Placement = pos=(0,0,0) rot=(1,0,0;1.5708rad)
  Profile = -> Sketch1401
  Reversed = true
  Type = 0
FEATURE [PartDesign::Body] Body307  label="red wire010"
  Group = -> [Sketch1401,Pad569]
  Origin = -> Origin442
  Placement = pos=(0,25.15,0) rot=(0,0,1;0rad)
  Tip = -> Pad569
FEATURE [Sketcher::SketchObject] Sketch1402
  MapMode = 5
  Support = -> [XY_Plane515]
  sketch-geometry (1):
    g0: Circle CenterX=0 CenterY=0 CenterZ=0 NormalX=0 NormalY=0 NormalZ=1 AngleXU=0 Radius=2.75
  constraints (2):
    c: Coincident(g0,g-1)
    c: Radius(g0) = 2.75
FEATURE [PartDesign::Pad] Pad571  label="M3x20 Head048"
  Length = 3
  Length2 = 100
  Profile = -> Sketch1402
  Type = 0
FEATURE [Sketcher::SketchObject] Sketch1403
  MapMode = 5
  Support = -> [XY_Plane532]
  sketch-geometry (1):
    g0: Circle CenterX=0 CenterY=0 CenterZ=0 NormalX=0 NormalY=0 NormalZ=1 AngleXU=0 Radius=2.75
  constraints (2):
    c: Coincident(g0,g-1)
    c: Radius(g0) = 2.75
FEATURE [PartDesign::Pad] Pad585  label="M3x20 Head051"
  Length = 3
  Length2 = 100
  Profile = -> Sketch1403
  Type = 0
FEATURE [Sketcher::SketchObject] Sketch1406
  MapMode = 5
  Placement = pos=(0,0,3) rot=(0,0,1;0rad)
  Support = -> [Pad571]
  sketch-geometry (1):
    g0: Circle CenterX=0 CenterY=0 CenterZ=0 NormalX=0 NormalY=0 NormalZ=1 AngleXU=0 Radius=1.5
  constraints (2):
    c: Coincident(g0,g-1)
    c: Radius(g0) = 1.5
FEATURE [PartDesign::Pad] Pad594  label="M3x20 Thread050"
  BaseFeature = -> Pad571
  Length = 20
  Length2 = 100
  Profile = -> Sketch1406
  Type = 0
FEATURE [Sketcher::SketchObject] Sketch1408
  MapMode = 5
  Placement = pos=(0,0,3) rot=(0,0,1;0rad)
  Support = -> [Pad585]
  sketch-geometry (1):
    g0: Circle CenterX=0 CenterY=0 CenterZ=0 NormalX=0 NormalY=0 NormalZ=1 AngleXU=0 Radius=1.5
  constraints (2):
    c: Coincident(g0,g-1)
    c: Radius(g0) = 1.5
FEATURE [PartDesign::Pad] Pad578  label="M3x20 Thread047"
  BaseFeature = -> Pad585
  Length = 20
  Length2 = 100
  Profile = -> Sketch1408
  Type = 0
FEATURE [Sketcher::SketchObject] Sketch1385
  MapMode = 5
  Placement = pos=(0,0,0) rot=(1,0,0;3.14159rad)
  Support = -> [Pad578]
  sketch-geometry (7):
    g0: LineSegment StartX=1.275 StartY=0.736122 StartZ=0 EndX=0 EndY=1.47224 EndZ=0
    g1: LineSegment StartX=0 StartY=1.47224 StartZ=0 EndX=-1.275 EndY=0.736122 EndZ=0
    g2: LineSegment StartX=-1.275 StartY=0.736122 StartZ=0 EndX=-1.275 EndY=-0.736122 EndZ=0
    g3: LineSegment StartX=-1.275 StartY=-0.736122 StartZ=0 EndX=1.34766e-11 EndY=-1.47224 EndZ=0
    g4: LineSegment StartX=1.34766e-11 StartY=-1.47224 StartZ=0 EndX=1.275 EndY=-0.736122 EndZ=0
    g5: LineSegment StartX=1.275 StartY=-0.736122 StartZ=0 EndX=1.275 EndY=0.736122 EndZ=0
    g6: Circle [constr] CenterX=0 CenterY=0 CenterZ=0 NormalX=0 NormalY=0 NormalZ=1 AngleXU=0 Radius=1.47224
  constraints (16):
    c: Coincident(g0,g1)
    c: Coincident(g1,g2)
    c: Coincident(g2,g3)
    c: Coincident(g3,g4)
    c: Coincident(g4,g5)
    c: Coincident(g5,g0)
    c: Equal(g0, g1-g5) x5
    c: PointOnObject(g0,g6)
    c: PointOnObject(g1,g6)
    c: PointOnObject(g2,g6)
    c: PointOnObject(g3,g6)
    c: PointOnObject(g4,g6)
    c: PointOnObject(g5,g6)
    c: Coincident(g6,g-1)
    c: PointOnObject(g0,g-2)
    c: DistanceX(g1,g0) = 2.55
FEATURE [PartDesign::Pocket] Pocket525  label="M3x20 Wrench052"
  BaseFeature = -> Pad578
  Length = 1.3
  Length2 = 100
  Profile = -> Sketch1385
  Type = 0
FEATURE [PartDesign::Chamfer] Chamfer253  label="M3x20 Smooth044"
  Base = -> Pocket525 [Face11,Edge2,Edge24,Edge3]
  BaseFeature = -> Pocket525
  Size = 0.2
FEATURE [PartDesign::Body] Body331  label="M3x068"
  Group = -> [Sketch1403,Pad585,Sketch1408,Pad578,Sketch1385,Pocket525,Chamfer253]
  Origin = -> Origin438
  Placement = pos=(-115.35,-29.35,62.05) rot=(-1,0,0;1.5708rad)
  Tip = -> Chamfer253
FEATURE [Sketcher::SketchObject] Sketch1415
  MapMode = 5
  Support = -> [XY_Plane542]
  sketch-geometry (1):
    g0: Circle CenterX=0 CenterY=0 CenterZ=0 NormalX=0 NormalY=0 NormalZ=1 AngleXU=0 Radius=2.75
  constraints (2):
    c: Coincident(g0,g-1)
    c: Radius(g0) = 2.75
FEATURE [PartDesign::Pad] Pad607  label="M3x20 Head055"
  Length = 3
  Length2 = 100
  Profile = -> Sketch1415
  Type = 0
FEATURE [Sketcher::SketchObject] Sketch1413
  MapMode = 5
  Placement = pos=(0,0,3) rot=(0,0,1;0rad)
  Support = -> [Pad607]
  sketch-geometry (1):
    g0: Circle CenterX=0 CenterY=0 CenterZ=0 NormalX=0 NormalY=0 NormalZ=1 AngleXU=0 Radius=1.5
  constraints (2):
    c: Coincident(g0,g-1)
    c: Radius(g0) = 1.5
FEATURE [PartDesign::Pad] Pad596  label="M3x20 Thread051"
  BaseFeature = -> Pad607
  Length = 20
  Length2 = 100
  Profile = -> Sketch1413
  Type = 0
FEATURE [Sketcher::SketchObject] Sketch1416
  MapMode = 5
  Placement = pos=(0,0,3) rot=(0,0,1;0rad)
  Support = -> [Pad583]
  sketch-geometry (1):
    g0: Circle CenterX=0 CenterY=0 CenterZ=0 NormalX=0 NormalY=0 NormalZ=1 AngleXU=0 Radius=1.5
  constraints (2):
    c: Coincident(g0,g-1)
    c: Radius(g0) = 1.5
FEATURE [PartDesign::Pad] Pad606  label="M3x20 Thread054"
  BaseFeature = -> Pad583
  Length = 20
  Length2 = 100
  Profile = -> Sketch1416
  Type = 0
FEATURE [Sketcher::SketchObject] Sketch1398
  MapMode = 5
  Placement = pos=(0,0,0) rot=(1,0,0;3.14159rad)
  Support = -> [Pad606]
  sketch-geometry (7):
    g0: LineSegment StartX=1.275 StartY=0.736122 StartZ=0 EndX=0 EndY=1.47224 EndZ=0
    g1: LineSegment StartX=0 StartY=1.47224 StartZ=0 EndX=-1.275 EndY=0.736122 EndZ=0
    g2: LineSegment StartX=-1.275 StartY=0.736122 StartZ=0 EndX=-1.275 EndY=-0.736122 EndZ=0
    g3: LineSegment StartX=-1.275 StartY=-0.736122 StartZ=0 EndX=1.34766e-11 EndY=-1.47224 EndZ=0
    g4: LineSegment StartX=1.34766e-11 StartY=-1.47224 StartZ=0 EndX=1.275 EndY=-0.736122 EndZ=0
    g5: LineSegment StartX=1.275 StartY=-0.736122 StartZ=0 EndX=1.275 EndY=0.736122 EndZ=0
    g6: Circle [constr] CenterX=0 CenterY=0 CenterZ=0 NormalX=0 NormalY=0 NormalZ=1 AngleXU=0 Radius=1.47224
  constraints (16):
    c: Coincident(g0,g1)
    c: Coincident(g1,g2)
    c: Coincident(g2,g3)
    c: Coincident(g3,g4)
    c: Coincident(g4,g5)
    c: Coincident(g5,g0)
    c: Equal(g0, g1-g5) x5
    c: PointOnObject(g0,g6)
    c: PointOnObject(g1,g6)
    c: PointOnObject(g2,g6)
    c: PointOnObject(g3,g6)
    c: PointOnObject(g4,g6)
    c: PointOnObject(g5,g6)
    c: Coincident(g6,g-1)
    c: PointOnObject(g0,g-2)
    c: DistanceX(g1,g0) = 2.55
FEATURE [PartDesign::Pocket] Pocket528  label="M3x20 Wrench053"
  BaseFeature = -> Pad606
  Length = 1.3
  Length2 = 100
  Profile = -> Sketch1398
  Type = 0
FEATURE [PartDesign::Chamfer] Chamfer255  label="M3x20 Smooth045"
  Base = -> Pocket528 [Face11,Edge2,Edge24,Edge3]
  BaseFeature = -> Pocket528
  Size = 0.2
FEATURE [PartDesign::Body] Body348  label="M3x073"
  Group = -> [Sketch1392,Pad583,Sketch1416,Pad606,Sketch1398,Pocket528,Chamfer255]
  Origin = -> Origin457
  Placement = pos=(-71.6,-25.55,52.05) rot=(-1,0,0;1.5708rad)
  Tip = -> Chamfer255
FEATURE [Sketcher::SketchObject] Sketch1417
  MapMode = 5
  Support = -> [XY_Plane538]
  sketch-geometry (1):
    g0: Circle CenterX=0 CenterY=0 CenterZ=0 NormalX=0 NormalY=0 NormalZ=1 AngleXU=0 Radius=2.75
  constraints (2):
    c: Coincident(g0,g-1)
    c: Radius(g0) = 2.75
FEATURE [PartDesign::Pad] Pad595  label="M3x20 Head053"
  Length = 3
  Length2 = 100
  Profile = -> Sketch1417
  Type = 0
FEATURE [Sketcher::SketchObject] Sketch1397
  MapMode = 5
  Placement = pos=(0,0,3) rot=(0,0,1;0rad)
  Support = -> [Pad595]
  sketch-geometry (1):
    g0: Circle CenterX=0 CenterY=0 CenterZ=0 NormalX=0 NormalY=0 NormalZ=1 AngleXU=0 Radius=1.5
  constraints (2):
    c: Coincident(g0,g-1)
    c: Radius(g0) = 1.5
FEATURE [PartDesign::Pad] Pad600  label="M3x20 Thread053"
  BaseFeature = -> Pad595
  Length = 20
  Length2 = 100
  Profile = -> Sketch1397
  Type = 0
FEATURE [Sketcher::SketchObject] Sketch1412
  MapMode = 5
  Placement = pos=(0,0,0) rot=(1,0,0;3.14159rad)
  Support = -> [Pad600]
  sketch-geometry (7):
    g0: LineSegment StartX=1.275 StartY=0.736122 StartZ=0 EndX=0 EndY=1.47224 EndZ=0
    g1: LineSegment StartX=0 StartY=1.47224 StartZ=0 EndX=-1.275 EndY=0.736122 EndZ=0
    g2: LineSegment StartX=-1.275 StartY=0.736122 StartZ=0 EndX=-1.275 EndY=-0.736122 EndZ=0
    g3: LineSegment StartX=-1.275 StartY=-0.736122 StartZ=0 EndX=1.34766e-11 EndY=-1.47224 EndZ=0
    g4: LineSegment StartX=1.34766e-11 StartY=-1.47224 StartZ=0 EndX=1.275 EndY=-0.736122 EndZ=0
    g5: LineSegment StartX=1.275 StartY=-0.736122 StartZ=0 EndX=1.275 EndY=0.736122 EndZ=0
    g6: Circle [constr] CenterX=0 CenterY=0 CenterZ=0 NormalX=0 NormalY=0 NormalZ=1 AngleXU=0 Radius=1.47224
  constraints (16):
    c: Coincident(g0,g1)
    c: Coincident(g1,g2)
    c: Coincident(g2,g3)
    c: Coincident(g3,g4)
    c: Coincident(g4,g5)
    c: Coincident(g5,g0)
    c: Equal(g0, g1-g5) x5
    c: PointOnObject(g0,g6)
    c: PointOnObject(g1,g6)
    c: PointOnObject(g2,g6)
    c: PointOnObject(g3,g6)
    c: PointOnObject(g4,g6)
    c: PointOnObject(g5,g6)
    c: Coincident(g6,g-1)
    c: PointOnObject(g0,g-2)
    c: DistanceX(g1,g0) = 2.55
FEATURE [PartDesign::Pocket] Pocket522  label="M3x20 Wrench050"
  BaseFeature = -> Pad600
  Length = 1.3
  Length2 = 100
  Profile = -> Sketch1412
  Type = 0
FEATURE [Sketcher::SketchObject] Sketch1418
  MapMode = 5
  Placement = pos=(0,0,2) rot=(0,0,1;0rad)
  Support = -> [Pad597]
  sketch-geometry (2):
    g0: Circle CenterX=0 CenterY=0 CenterZ=0 NormalX=0 NormalY=0 NormalZ=1 AngleXU=0 Radius=5
    g1: Circle CenterX=0 CenterY=0 CenterZ=0 NormalX=0 NormalY=0 NormalZ=1 AngleXU=0 Radius=3.5
  constraints (4):
    c: Coincident(g0,g-1)
    c: Coincident(g1,g0)
    c: Radius(g1) = 3.5
    c: Radius(g0) = 5
FEATURE [PartDesign::Pocket] Pocket541
  BaseFeature = -> Pad597
  Length = 1
  Length2 = 100
  Profile = -> Sketch1418
  Type = 0
FEATURE [Sketcher::SketchObject] Sketch1248
  MapMode = 5
  Placement = pos=(0,0,2) rot=(0,0,1;0rad)
  Support = -> [Pocket541]
  sketch-geometry (1):
    g0: Circle CenterX=0 CenterY=0 CenterZ=0 NormalX=0 NormalY=0 NormalZ=1 AngleXU=0 Radius=3
  constraints (2):
    c: Coincident(g0,g-1)
    c: Radius(g0) = 3
FEATURE [PartDesign::Pocket] Pocket531
  BaseFeature = -> Pocket541
  Length = 1
  Length2 = 100
  Profile = -> Sketch1248
  Type = 0
FEATURE [Sketcher::SketchObject] Sketch1243
  MapMode = 5
  Placement = pos=(0,0,1) rot=(0,0,1;0rad)
  Support = -> [Pocket531]
  sketch-geometry (1):
    g0: Circle CenterX=0 CenterY=0 CenterZ=0 NormalX=0 NormalY=0 NormalZ=1 AngleXU=0 Radius=1.5
  constraints (2):
    c: Coincident(g0,g-1)
    c: Radius(g0) = 1.5
FEATURE [PartDesign::Pocket] Pocket530
  BaseFeature = -> Pocket531
  Length = 5
  Length2 = 100
  Profile = -> Sketch1243
  Type = 0
FEATURE [Sketcher::SketchObject] Sketch1230
  MapMode = 5
  Placement = pos=(0,0,0) rot=(1,0,0;3.14159rad)
  Support = -> [Pocket530]
  sketch-geometry (2):
    g0: Circle CenterX=0 CenterY=0 CenterZ=0 NormalX=0 NormalY=0 NormalZ=1 AngleXU=0 Radius=4.5
    g1: Circle CenterX=0 CenterY=0 CenterZ=0 NormalX=0 NormalY=0 NormalZ=1 AngleXU=0 Radius=3
  constraints (4):
    c: Coincident(g0,g-1)
    c: Coincident(g1,g0)
    c: Radius(g0) = 4.5
    c: Radius(g1) = 3
FEATURE [PartDesign::Pad] Pad621
  BaseFeature = -> Pocket530
  Length = 3
  Length2 = 100
  Profile = -> Sketch1230
  Type = 0
FEATURE [PartDesign::Fillet] Fillet158
  Base = -> Pad621 [Face5,Edge96,Face4]
  BaseFeature = -> Pad621
  Radius = 0.2
FEATURE [Sketcher::SketchObject] Sketch1266
  ExternalGeometry = -> [Fillet158]
  MapMode = 5
  Support = -> [XY_Plane530]
  sketch-geometry (3):
    g0: ArcOfCircle [constr] CenterX=-2e-16 CenterY=-3e-16 CenterZ=0 NormalX=0 NormalY=0 NormalZ=1 AngleXU=0 Radius=13.5 StartAngle=3.66519 EndAngle=5.75959
    g1: ArcOfCircle [constr] CenterX=-2e-16 CenterY=-3e-16 CenterZ=0 NormalX=0 NormalY=0 NormalZ=1 AngleXU=0 Radius=13.5 StartAngle=2.61799 EndAngle=3.66519
    g2: LineSegment StartX=-11.6913 StartY=-6.75 StartZ=0 EndX=11.6913 EndY=6.75 EndZ=0
  constraints (9):
    c: Coincident(g0,g-5)
    c: Coincident(g0,g-4)
    c: Coincident(g1,g0)
    c: Coincident(g1,g0)
    c: Angle(g0) = 2.0944
    c: Angle(g1) = 1.0472
    c: Coincident(g1,g-3)
    c: Coincident(g2,g0)
    c: Coincident(g2,g-6)
FEATURE [Sketcher::SketchObject] Sketch1419
  MapMode = 5
  Placement = pos=(0,0,3) rot=(0,0,1;0rad)
  Support = -> [Pad573]
  sketch-geometry (1):
    g0: Circle CenterX=0 CenterY=0 CenterZ=0 NormalX=0 NormalY=0 NormalZ=1 AngleXU=0 Radius=1.5
  constraints (2):
    c: Coincident(g0,g-1)
    c: Radius(g0) = 1.5
FEATURE [PartDesign::Pad] Pad579  label="M3x20 Thread048"
  BaseFeature = -> Pad573
  Length = 20
  Length2 = 100
  Profile = -> Sketch1419
  Type = 0
FEATURE [Sketcher::SketchObject] Sketch1420
  MapMode = 5
  Placement = pos=(0,0,0) rot=(1,0,0;3.14159rad)
  Support = -> [Pad594]
  sketch-geometry (7):
    g0: LineSegment StartX=1.275 StartY=0.736122 StartZ=0 EndX=0 EndY=1.47224 EndZ=0
    g1: LineSegment StartX=0 StartY=1.47224 StartZ=0 EndX=-1.275 EndY=0.736122 EndZ=0
    g2: LineSegment StartX=-1.275 StartY=0.736122 StartZ=0 EndX=-1.275 EndY=-0.736122 EndZ=0
    g3: LineSegment StartX=-1.275 StartY=-0.736122 StartZ=0 EndX=1.34766e-11 EndY=-1.47224 EndZ=0
    g4: LineSegment StartX=1.34766e-11 StartY=-1.47224 StartZ=0 EndX=1.275 EndY=-0.736122 EndZ=0
    g5: LineSegment StartX=1.275 StartY=-0.736122 StartZ=0 EndX=1.275 EndY=0.736122 EndZ=0
    g6: Circle [constr] CenterX=0 CenterY=0 CenterZ=0 NormalX=0 NormalY=0 NormalZ=1 AngleXU=0 Radius=1.47224
  constraints (16):
    c: Coincident(g0,g1)
    c: Coincident(g1,g2)
    c: Coincident(g2,g3)
    c: Coincident(g3,g4)
    c: Coincident(g4,g5)
    c: Coincident(g5,g0)
    c: Equal(g0, g1-g5) x5
    c: PointOnObject(g0,g6)
    c: PointOnObject(g1,g6)
    c: PointOnObject(g2,g6)
    c: PointOnObject(g3,g6)
    c: PointOnObject(g4,g6)
    c: PointOnObject(g5,g6)
    c: Coincident(g6,g-1)
    c: PointOnObject(g0,g-2)
    c: DistanceX(g1,g0) = 2.55
FEATURE [PartDesign::Pocket] Pocket524  label="M3x20 Wrench051"
  BaseFeature = -> Pad594
  Length = 1.3
  Length2 = 100
  Profile = -> Sketch1420
  Type = 0
FEATURE [PartDesign::Chamfer] Chamfer251  label="M3x20 Smooth043"
  Base = -> Pocket524 [Face11,Edge2,Edge24,Edge3]
  BaseFeature = -> Pocket524
  Size = 0.2
FEATURE [PartDesign::Body] Body345  label="M3x072"
  Group = -> [Sketch1402,Pad571,Sketch1406,Pad594,Sketch1420,Pocket524,Chamfer251]
  Origin = -> Origin493
  Placement = pos=(-110.55,28,52.05) rot=(1,0,0;1.5708rad)
  Tip = -> Chamfer251
FEATURE [Sketcher::SketchObject] Sketch1421
  MapMode = 5
  Placement = pos=(0,0,5) rot=(0,0,1;0rad)
  Support = -> [Pocket538]
  sketch-geometry (9):
    g0: Circle [constr] CenterX=0 CenterY=0 CenterZ=0 NormalX=0 NormalY=0 NormalZ=1 AngleXU=0 Radius=20
    g1: LineSegment [constr] StartX=-14.1421 StartY=14.1421 StartZ=0 EndX=14.1421 EndY=14.1421 EndZ=0
    g2: LineSegment [constr] StartX=14.1421 StartY=14.1421 StartZ=0 EndX=14.1421 EndY=-14.1421 EndZ=0
    g3: LineSegment [constr] StartX=14.1421 StartY=-14.1421 StartZ=0 EndX=-14.1421 EndY=-14.1421 EndZ=0
    g4: LineSegment [constr] StartX=-14.1421 StartY=-14.1421 StartZ=0 EndX=-14.1421 EndY=14.1421 EndZ=0
    g5: Circle CenterX=-14.1421 CenterY=14.1421 CenterZ=0 NormalX=0 NormalY=0 NormalZ=1 AngleXU=0 Radius=1.6
    g6: Circle CenterX=14.1421 CenterY=14.1421 CenterZ=0 NormalX=0 NormalY=0 NormalZ=1 AngleXU=0 Radius=1.6
    g7: Circle CenterX=14.1421 CenterY=-14.1421 CenterZ=0 NormalX=0 NormalY=0 NormalZ=1 AngleXU=0 Radius=1.6
    g8: Circle CenterX=-14.1421 CenterY=-14.1421 CenterZ=0 NormalX=0 NormalY=0 NormalZ=1 AngleXU=0 Radius=1.6
  constraints (22):
    c: Coincident(g0,g-1)
    c: Radius(g0) = 20
    c: Coincident(g1,g2)
    c: Coincident(g2,g3)
    c: Coincident(g3,g4)
    c: Coincident(g4,g1)
    c: Horizontal(g1)
    c: Horizontal(g3)
    c: Vertical(g2)
    c: Vertical(g4)
    c: PointOnObject(g1,g0)
    c: PointOnObject(g2,g0)
    c: PointOnObject(g1,g0)
    c: Equal(g1,g2)
    c: Coincident(g5,g1)
    c: Coincident(g6,g1)
    c: Coincident(g7,g2)
    c: Coincident(g8,g3)
    c: Radius(g5) = 1.6
    c: Equal(g5,g6)
    c: Equal(g5,g7)
    c: Equal(g5,g8)
FEATURE [PartDesign::Pocket] Pocket533  label="Screwholes Servohorn Cap002"
  BaseFeature = -> Pocket538
  Length = 5
  Length2 = 100
  Profile = -> Sketch1421
  Type = 0
FEATURE [Sketcher::SketchObject] Sketch1249
  MapMode = 5
  Placement = pos=(0,0,5) rot=(0,0,1;0rad)
  Support = -> [Pocket533]
  sketch-geometry (35):
    g0: Circle [constr] CenterX=0 CenterY=0 CenterZ=0 NormalX=0 NormalY=0 NormalZ=1 AngleXU=0 Radius=20
    g1: LineSegment [constr] StartX=-14.1421 StartY=14.1421 StartZ=0 EndX=14.1421 EndY=-14.1421 EndZ=0
    g2: LineSegment [constr] StartX=14.1421 StartY=14.1421 StartZ=0 EndX=-14.1421 EndY=-14.1421 EndZ=0
    g3: LineSegment [constr] StartX=-14.1421 StartY=14.1421 StartZ=0 EndX=14.1421 EndY=14.1421 EndZ=0
    g4: LineSegment [constr] StartX=14.1421 StartY=14.1421 StartZ=0 EndX=14.1421 EndY=-14.1421 EndZ=0
    g5: LineSegment [constr] StartX=14.1421 StartY=-14.1421 StartZ=0 EndX=-14.1421 EndY=-14.1421 EndZ=0
    g6: LineSegment [constr] StartX=-14.1421 StartY=-14.1421 StartZ=0 EndX=-14.1421 EndY=14.1421 EndZ=0
    g7: LineSegment StartX=-11.8151 StartY=16.4692 StartZ=0 EndX=-14.9939 EndY=17.3209 EndZ=0
    g8: LineSegment StartX=-14.9939 StartY=17.3209 StartZ=0 EndX=-17.3209 EndY=14.9939 EndZ=0
    g9: LineSegment StartX=-17.3209 StartY=14.9939 StartZ=0 EndX=-16.4692 EndY=11.8151 EndZ=0
    g10: LineSegment StartX=-16.4692 StartY=11.8151 StartZ=0 EndX=-13.2904 EndY=10.9634 EndZ=0
    g11: LineSegment StartX=-13.2904 StartY=10.9634 StartZ=0 EndX=-10.9634 EndY=13.2904 EndZ=0
    g12: LineSegment StartX=-10.9634 StartY=13.2904 StartZ=0 EndX=-11.8151 EndY=16.4692 EndZ=0
    g13: Circle [constr] CenterX=-14.1421 CenterY=14.1421 CenterZ=0 NormalX=0 NormalY=0 NormalZ=1 AngleXU=0 Radius=3.2909
    g14: LineSegment StartX=14.9939 StartY=17.3209 StartZ=0 EndX=11.8151 EndY=16.4692 EndZ=0
    g15: LineSegment StartX=11.8151 StartY=16.4692 StartZ=0 EndX=10.9634 EndY=13.2904 EndZ=0
    g16: LineSegment StartX=10.9634 StartY=13.2904 StartZ=0 EndX=13.2904 EndY=10.9634 EndZ=0
    g17: LineSegment StartX=13.2904 StartY=10.9634 StartZ=0 EndX=16.4692 EndY=11.8151 EndZ=0
    g18: LineSegment StartX=16.4692 StartY=11.8151 StartZ=0 EndX=17.3209 EndY=14.9939 EndZ=0
    g19: LineSegment StartX=17.3209 StartY=14.9939 StartZ=0 EndX=14.9939 EndY=17.3209 EndZ=0
    g20: Circle [constr] CenterX=14.1421 CenterY=14.1421 CenterZ=0 NormalX=0 NormalY=0 NormalZ=1 AngleXU=0 Radius=3.2909
    g21: LineSegment StartX=-13.2904 StartY=-10.9634 StartZ=0 EndX=-16.4692 EndY=-11.8151 EndZ=0
    g22: LineSegment StartX=-16.4692 StartY=-11.8151 StartZ=0 EndX=-17.3209 EndY=-14.9939 EndZ=0
    g23: LineSegment StartX=-17.3209 StartY=-14.9939 StartZ=0 EndX=-14.9939 EndY=-17.3209 EndZ=0
    g24: LineSegment StartX=-14.9939 StartY=-17.3209 StartZ=0 EndX=-11.8151 EndY=-16.4692 EndZ=0
    g25: LineSegment StartX=-11.8151 StartY=-16.4692 StartZ=0 EndX=-10.9634 EndY=-13.2904 EndZ=0
    g26: LineSegment StartX=-10.9634 StartY=-13.2904 StartZ=0 EndX=-13.2904 EndY=-10.9634 EndZ=0
    g27: Circle [constr] CenterX=-14.1421 CenterY=-14.1421 CenterZ=0 NormalX=0 NormalY=0 NormalZ=1 AngleXU=0 Radius=3.2909
    g28: LineSegment StartX=16.4692 StartY=-11.8151 StartZ=0 EndX=13.2904 EndY=-10.9634 EndZ=0
    g29: LineSegment StartX=13.2904 StartY=-10.9634 StartZ=0 EndX=10.9634 EndY=-13.2904 EndZ=0
    g30: LineSegment StartX=10.9634 StartY=-13.2904 StartZ=0 EndX=11.8151 EndY=-16.4692 EndZ=0
    g31: LineSegment StartX=11.8151 StartY=-16.4692 StartZ=0 EndX=14.9939 EndY=-17.3209 EndZ=0
    g32: LineSegment StartX=14.9939 StartY=-17.3209 StartZ=0 EndX=17.3209 EndY=-14.9939 EndZ=0
    g33: LineSegment StartX=17.3209 StartY=-14.9939 StartZ=0 EndX=16.4692 EndY=-11.8151 EndZ=0
    g34: Circle [constr] CenterX=14.1421 CenterY=-14.1421 CenterZ=0 NormalX=0 NormalY=0 NormalZ=1 AngleXU=0 Radius=3.2909
  constraints (84):
    c: Coincident(g0,g-1)
    c: Radius(g0) = 20
    c: PointOnObject(g1,g0)
    c: PointOnObject(g1,g0)
    c: PointOnObject(g2,g0)
    c: PointOnObject(g2,g0)
    c: PointOnObject(g-1,g2)
    c: PointOnObject(g-1,g1)
    c: Perpendicular(g1,g2)
    c: Coincident(g3,g4)
    c: Coincident(g4,g5)
    c: Coincident(g5,g6)
    c: Coincident(g6,g3)
    c: Horizontal(g3)
    c: Horizontal(g5)
    c: Vertical(g4)
    c: Vertical(g6)
    c: Coincident(g3,g1)
    c: Coincident(g4,g1)
    c: Equal(g3,g4)
    c: Coincident(g7,g8)
    c: Coincident(g8,g9)
    c: Coincident(g9,g10)
    c: Coincident(g10,g11)
    c: Coincident(g11,g12)
    c: Coincident(g12,g7)
    c: Equal(g7, g8-g12) x5
    c: PointOnObject(g7,g13)
    c: PointOnObject(g8,g13)
    c: PointOnObject(g9,g13)
    c: PointOnObject(g10,g13)
    c: PointOnObject(g11,g13)
    c: PointOnObject(g12,g13)
    c: Coincident(g13,g1)
    c: Coincident(g14,g15)
    c: Coincident(g15,g16)
    c: Coincident(g16,g17)
    c: Coincident(g17,g18)
    c: Coincident(g18,g19)
    c: Coincident(g19,g14)
    c: Equal(g14, g15-g19) x5
    c: PointOnObject(g14,g20)
    c: PointOnObject(g15,g20)
    c: PointOnObject(g16,g20)
    c: PointOnObject(g17,g20)
    c: PointOnObject(g18,g20)
    c: PointOnObject(g19,g20)
    c: Coincident(g20,g2)
    c: Coincident(g21,g22)
    c: Coincident(g22,g23)
    c: Coincident(g23,g24)
    c: Coincident(g24,g25)
    c: Coincident(g25,g26)
    c: Coincident(g26,g21)
    c: Equal(g21, g22-g26) x5
    c: PointOnObject(g21,g27)
    c: PointOnObject(g22,g27)
    c: PointOnObject(g23,g27)
    c: PointOnObject(g24,g27)
    c: PointOnObject(g25,g27)
    c: PointOnObject(g26,g27)
    c: Coincident(g27,g2)
    c: Perpendicular(g1,g11)
    c: Perpendicular(g2,g16)
    c: Perpendicular(g2,g26)
    c: Coincident(g28,g29)
    c: Coincident(g29,g30)
    c: Coincident(g30,g31)
    c: Coincident(g31,g32)
    c: Coincident(g32,g33)
    c: Coincident(g33,g28)
    c: Equal(g28, g29-g33) x5
    c: PointOnObject(g28,g34)
    c: PointOnObject(g29,g34)
    c: PointOnObject(g30,g34)
    c: PointOnObject(g31,g34)
    c: PointOnObject(g32,g34)
    c: PointOnObject(g33,g34)
    c: Coincident(g34,g1)
    c: Perpendicular(g1,g29)
    c: Equal(g20,g13)
    c: Equal(g13,g27)
    c: Equal(g27,g34)
    c: Distance(g15,g14) = 5.7
FEATURE [PartDesign::Pocket] Pocket551  label="Nutholes Servohorn Cap002"
  BaseFeature = -> Pocket533
  Length = 2.5
  Length2 = 100
  Profile = -> Sketch1249
  Type = 0
FEATURE [Sketcher::SketchObject] Sketch1422
  MapMode = 5
  Support = -> [XY_Plane534]
  sketch-geometry (1):
    g0: Circle CenterX=0 CenterY=0 CenterZ=0 NormalX=0 NormalY=0 NormalZ=1 AngleXU=0 Radius=2.75
  constraints (2):
    c: Coincident(g0,g-1)
    c: Radius(g0) = 2.75
FEATURE [PartDesign::Pad] Pad593  label="M3x20 Head052"
  Length = 3
  Length2 = 100
  Profile = -> Sketch1422
  Type = 0
FEATURE [Sketcher::SketchObject] Sketch1409
  MapMode = 5
  Placement = pos=(0,0,3) rot=(0,0,1;0rad)
  Support = -> [Pad593]
  sketch-geometry (1):
    g0: Circle CenterX=0 CenterY=0 CenterZ=0 NormalX=0 NormalY=0 NormalZ=1 AngleXU=0 Radius=1.5
  constraints (2):
    c: Coincident(g0,g-1)
    c: Radius(g0) = 1.5
FEATURE [PartDesign::Pad] Pad587  label="M3x20 Thread049"
  BaseFeature = -> Pad593
  Length = 20
  Length2 = 100
  Profile = -> Sketch1409
  Type = 0
FEATURE [Sketcher::SketchObject] Sketch1388
  MapMode = 5
  Placement = pos=(0,0,0) rot=(1,0,0;3.14159rad)
  Support = -> [Pad587]
  sketch-geometry (7):
    g0: LineSegment StartX=1.275 StartY=0.736122 StartZ=0 EndX=0 EndY=1.47224 EndZ=0
    g1: LineSegment StartX=0 StartY=1.47224 StartZ=0 EndX=-1.275 EndY=0.736122 EndZ=0
    g2: LineSegment StartX=-1.275 StartY=0.736122 StartZ=0 EndX=-1.275 EndY=-0.736122 EndZ=0
    g3: LineSegment StartX=-1.275 StartY=-0.736122 StartZ=0 EndX=1.34766e-11 EndY=-1.47224 EndZ=0
    g4: LineSegment StartX=1.34766e-11 StartY=-1.47224 StartZ=0 EndX=1.275 EndY=-0.736122 EndZ=0
    g5: LineSegment StartX=1.275 StartY=-0.736122 StartZ=0 EndX=1.275 EndY=0.736122 EndZ=0
    g6: Circle [constr] CenterX=0 CenterY=0 CenterZ=0 NormalX=0 NormalY=0 NormalZ=1 AngleXU=0 Radius=1.47224
  constraints (16):
    c: Coincident(g0,g1)
    c: Coincident(g1,g2)
    c: Coincident(g2,g3)
    c: Coincident(g3,g4)
    c: Coincident(g4,g5)
    c: Coincident(g5,g0)
    c: Equal(g0, g1-g5) x5
    c: PointOnObject(g0,g6)
    c: PointOnObject(g1,g6)
    c: PointOnObject(g2,g6)
    c: PointOnObject(g3,g6)
    c: PointOnObject(g4,g6)
    c: PointOnObject(g5,g6)
    c: Coincident(g6,g-1)
    c: PointOnObject(g0,g-2)
    c: DistanceX(g1,g0) = 2.55
FEATURE [PartDesign::Pocket] Pocket516  label="M3x20 Wrench048"
  BaseFeature = -> Pad587
  Length = 1.3
  Length2 = 100
  Profile = -> Sketch1388
  Type = 0
FEATURE [Sketcher::SketchObject] Sketch1423
  MapMode = 5
  Placement = pos=(0,0,0) rot=(1,0,0;3.14159rad)
  Support = -> [Pad579]
  sketch-geometry (7):
    g0: LineSegment StartX=1.275 StartY=0.736122 StartZ=0 EndX=0 EndY=1.47224 EndZ=0
    g1: LineSegment StartX=0 StartY=1.47224 StartZ=0 EndX=-1.275 EndY=0.736122 EndZ=0
    g2: LineSegment StartX=-1.275 StartY=0.736122 StartZ=0 EndX=-1.275 EndY=-0.736122 EndZ=0
    g3: LineSegment StartX=-1.275 StartY=-0.736122 StartZ=0 EndX=1.34766e-11 EndY=-1.47224 EndZ=0
    g4: LineSegment StartX=1.34766e-11 StartY=-1.47224 StartZ=0 EndX=1.275 EndY=-0.736122 EndZ=0
    g5: LineSegment StartX=1.275 StartY=-0.736122 StartZ=0 EndX=1.275 EndY=0.736122 EndZ=0
    g6: Circle [constr] CenterX=0 CenterY=0 CenterZ=0 NormalX=0 NormalY=0 NormalZ=1 AngleXU=0 Radius=1.47224
  constraints (16):
    c: Coincident(g0,g1)
    c: Coincident(g1,g2)
    c: Coincident(g2,g3)
    c: Coincident(g3,g4)
    c: Coincident(g4,g5)
    c: Coincident(g5,g0)
    c: Equal(g0, g1-g5) x5
    c: PointOnObject(g0,g6)
    c: PointOnObject(g1,g6)
    c: PointOnObject(g2,g6)
    c: PointOnObject(g3,g6)
    c: PointOnObject(g4,g6)
    c: PointOnObject(g5,g6)
    c: Coincident(g6,g-1)
    c: PointOnObject(g0,g-2)
    c: DistanceX(g1,g0) = 2.55
FEATURE [PartDesign::Pocket] Pocket534  label="M3x20 Wrench054"
  BaseFeature = -> Pad579
  Length = 1.3
  Length2 = 100
  Profile = -> Sketch1423
  Type = 0
FEATURE [Sketcher::SketchObject] Sketch1424
  MapMode = 5
  Support = -> [XY_Plane526]
  sketch-geometry (1):
    g0: Circle CenterX=0 CenterY=0 CenterZ=0 NormalX=0 NormalY=0 NormalZ=1 AngleXU=0 Radius=2.75
  constraints (2):
    c: Coincident(g0,g-1)
    c: Radius(g0) = 2.75
FEATURE [PartDesign::Pad] Pad604  label="M3x8 Head069"
  Length = 3
  Length2 = 100
  Profile = -> Sketch1424
  Type = 0
FEATURE [Sketcher::SketchObject] Sketch1411
  MapMode = 5
  Placement = pos=(0,0,3) rot=(0,0,1;0rad)
  Support = -> [Pad604]
  sketch-geometry (1):
    g0: Circle CenterX=0 CenterY=0 CenterZ=0 NormalX=0 NormalY=0 NormalZ=1 AngleXU=0 Radius=1.5
  constraints (2):
    c: Coincident(g0,g-1)
    c: Radius(g0) = 1.5
FEATURE [PartDesign::Pad] Pad588  label="M3x8 Thread066"
  BaseFeature = -> Pad604
  Length = 8
  Length2 = 100
  Profile = -> Sketch1411
  Type = 0
FEATURE [Sketcher::SketchObject] Sketch1410
  MapMode = 5
  Placement = pos=(0,0,0) rot=(1,0,0;3.14159rad)
  Support = -> [Pad588]
  sketch-geometry (7):
    g0: LineSegment StartX=1.275 StartY=0.736122 StartZ=0 EndX=0 EndY=1.47224 EndZ=0
    g1: LineSegment StartX=0 StartY=1.47224 StartZ=0 EndX=-1.275 EndY=0.736122 EndZ=0
    g2: LineSegment StartX=-1.275 StartY=0.736122 StartZ=0 EndX=-1.275 EndY=-0.736122 EndZ=0
    g3: LineSegment StartX=-1.275 StartY=-0.736122 StartZ=0 EndX=1.34766e-11 EndY=-1.47224 EndZ=0
    g4: LineSegment StartX=1.34766e-11 StartY=-1.47224 StartZ=0 EndX=1.275 EndY=-0.736122 EndZ=0
    g5: LineSegment StartX=1.275 StartY=-0.736122 StartZ=0 EndX=1.275 EndY=0.736122 EndZ=0
    g6: Circle [constr] CenterX=0 CenterY=0 CenterZ=0 NormalX=0 NormalY=0 NormalZ=1 AngleXU=0 Radius=1.47224
  constraints (16):
    c: Coincident(g0,g1)
    c: Coincident(g1,g2)
    c: Coincident(g2,g3)
    c: Coincident(g3,g4)
    c: Coincident(g4,g5)
    c: Coincident(g5,g0)
    c: Equal(g0, g1-g5) x5
    c: PointOnObject(g0,g6)
    c: PointOnObject(g1,g6)
    c: PointOnObject(g2,g6)
    c: PointOnObject(g3,g6)
    c: PointOnObject(g4,g6)
    c: PointOnObject(g5,g6)
    c: Coincident(g6,g-1)
    c: PointOnObject(g0,g-2)
    c: DistanceX(g1,g0) = 2.55
FEATURE [PartDesign::Pocket] Pocket521  label="M3x8 Wrench066"
  BaseFeature = -> Pad588
  Length = 1.3
  Length2 = 100
  Profile = -> Sketch1410
  Type = 0
FEATURE [PartDesign::Chamfer] Chamfer229  label="M3x8 Smooth060"
  Base = -> Pocket521 [Face11,Edge2,Edge24,Edge3]
  BaseFeature = -> Pocket521
  Size = 0.2
FEATURE [PartDesign::Body] Body384  label="M3x082"
  Group = -> [Sketch1424,Pad604,Sketch1411,Pad588,Sketch1410,Pocket521,Chamfer229]
  Origin = -> Origin452
  Placement = pos=(-144.1,30.35,27.05) rot=(0,0.707107,-0.707107;3.14159rad)
  Tip = -> Chamfer229
FEATURE [Sketcher::SketchObject] Sketch1425
  MapMode = 5
  Placement = pos=(0,0,0) rot=(1,0,0;3.14159rad)
  Support = -> [Pad596]
  sketch-geometry (7):
    g0: LineSegment StartX=1.275 StartY=0.736122 StartZ=0 EndX=0 EndY=1.47224 EndZ=0
    g1: LineSegment StartX=0 StartY=1.47224 StartZ=0 EndX=-1.275 EndY=0.736122 EndZ=0
    g2: LineSegment StartX=-1.275 StartY=0.736122 StartZ=0 EndX=-1.275 EndY=-0.736122 EndZ=0
    g3: LineSegment StartX=-1.275 StartY=-0.736122 StartZ=0 EndX=1.34766e-11 EndY=-1.47224 EndZ=0
    g4: LineSegment StartX=1.34766e-11 StartY=-1.47224 StartZ=0 EndX=1.275 EndY=-0.736122 EndZ=0
    g5: LineSegment StartX=1.275 StartY=-0.736122 StartZ=0 EndX=1.275 EndY=0.736122 EndZ=0
    g6: Circle [constr] CenterX=0 CenterY=0 CenterZ=0 NormalX=0 NormalY=0 NormalZ=1 AngleXU=0 Radius=1.47224
  constraints (16):
    c: Coincident(g0,g1)
    c: Coincident(g1,g2)
    c: Coincident(g2,g3)
    c: Coincident(g3,g4)
    c: Coincident(g4,g5)
    c: Coincident(g5,g0)
    c: Equal(g0, g1-g5) x5
    c: PointOnObject(g0,g6)
    c: PointOnObject(g1,g6)
    c: PointOnObject(g2,g6)
    c: PointOnObject(g3,g6)
    c: PointOnObject(g4,g6)
    c: PointOnObject(g5,g6)
    c: Coincident(g6,g-1)
    c: PointOnObject(g0,g-2)
    c: DistanceX(g1,g0) = 2.55
FEATURE [PartDesign::Pocket] Pocket515  label="M3x20 Wrench047"
  BaseFeature = -> Pad596
  Length = 1.3
  Length2 = 100
  Profile = -> Sketch1425
  Type = 0
FEATURE [PartDesign::Chamfer] Chamfer245  label="M3x20 Smooth042"
  Base = -> Pocket515 [Face11,Edge2,Edge24,Edge3]
  BaseFeature = -> Pocket515
  Size = 0.2
FEATURE [PartDesign::Body] Body334  label="M3x069"
  Group = -> [Sketch1415,Pad607,Sketch1413,Pad596,Sketch1425,Pocket515,Chamfer245]
  Origin = -> Origin486
  Placement = pos=(-23.1,-25.6,52) rot=(-1,0,0;1.5708rad)
  Tip = -> Chamfer245
FEATURE [Sketcher::SketchObject] Sketch1426
  MapMode = 5
  Support = -> [XY_Plane535]
  sketch-geometry (1):
    g0: Circle CenterX=0 CenterY=0 CenterZ=0 NormalX=0 NormalY=0 NormalZ=1 AngleXU=0 Radius=2.75
  constraints (2):
    c: Coincident(g0,g-1)
    c: Radius(g0) = 2.75
FEATURE [PartDesign::Pad] Pad601  label="M3x20 Head054"
  Length = 3
  Length2 = 100
  Profile = -> Sketch1426
  Type = 0
FEATURE [Sketcher::SketchObject] Sketch1414
  MapMode = 5
  Placement = pos=(0,0,3) rot=(0,0,1;0rad)
  Support = -> [Pad601]
  sketch-geometry (1):
    g0: Circle CenterX=0 CenterY=0 CenterZ=0 NormalX=0 NormalY=0 NormalZ=1 AngleXU=0 Radius=1.5
  constraints (2):
    c: Coincident(g0,g-1)
    c: Radius(g0) = 1.5
FEATURE [PartDesign::Pad] Pad599  label="M3x20 Thread052"
  BaseFeature = -> Pad601
  Length = 20
  Length2 = 100
  Profile = -> Sketch1414
  Type = 0
FEATURE [Sketcher::SketchObject] Sketch1428
  MapMode = 5
  Placement = pos=(0,0,5) rot=(0,0,1;0rad)
  Support = -> [Pocket560]
  sketch-geometry (1):
    g0: Circle CenterX=0 CenterY=0 CenterZ=0 NormalX=0 NormalY=0 NormalZ=1 AngleXU=0 Radius=6.15
  constraints (2):
    c: Coincident(g0,g-1)
    c: Radius(g0) = 6.15
FEATURE [PartDesign::Pocket] Pocket553  label="Servohole002"
  BaseFeature = -> Pocket560
  Length = 5
  Length2 = 100
  Profile = -> Sketch1428
  Type = 0
FEATURE [Sketcher::SketchObject] Sketch1260
  MapMode = 5
  Placement = pos=(0,0,5) rot=(0,0,1;0rad)
  Support = -> [Pocket553]
  sketch-geometry (32):
    g0: LineSegment [constr] StartX=3.75 StartY=6.49519 StartZ=0 EndX=-3.75 EndY=6.49519 EndZ=0
    g1: LineSegment [constr] StartX=-3.75 StartY=6.49519 StartZ=0 EndX=-7.5 EndY=9e-16 EndZ=0
    g2: LineSegment [constr] StartX=-7.5 StartY=9e-16 StartZ=0 EndX=-3.75 EndY=-6.49519 EndZ=0
    g3: LineSegment [constr] StartX=-3.75 StartY=-6.49519 StartZ=0 EndX=3.75 EndY=-6.49519 EndZ=0
    g4: LineSegment [constr] StartX=3.75 StartY=-6.49519 StartZ=0 EndX=7.5 EndY=0 EndZ=0
    g5: LineSegment [constr] StartX=7.5 StartY=0 StartZ=0 EndX=3.75 EndY=6.49519 EndZ=0
    g6: Circle [constr] CenterX=0 CenterY=0 CenterZ=0 NormalX=0 NormalY=0 NormalZ=1 AngleXU=0 Radius=7.5
    g7: LineSegment [constr] StartX=0 StartY=13.5 StartZ=0 EndX=-11.6913 EndY=6.75 EndZ=0
    g8: LineSegment [constr] StartX=-11.6913 StartY=6.75 StartZ=0 EndX=-11.6913 EndY=-6.75 EndZ=0
    g9: LineSegment [constr] StartX=-11.6913 StartY=-6.75 StartZ=0 EndX=0 EndY=-13.5 EndZ=0
    g10: LineSegment [constr] StartX=-5e-16 StartY=-13.5 StartZ=0 EndX=11.6913 EndY=-6.75 EndZ=0
    g11: LineSegment [constr] StartX=11.6913 StartY=-6.75 StartZ=0 EndX=11.6913 EndY=6.75 EndZ=0
    g12: LineSegment [constr] StartX=11.6913 StartY=6.75 StartZ=0 EndX=0 EndY=13.5 EndZ=0
    g13: Circle [constr] CenterX=0 CenterY=0 CenterZ=0 NormalX=0 NormalY=0 NormalZ=1 AngleXU=0 Radius=13.5
    g14: ArcOfCircle CenterX=0 CenterY=13.5 CenterZ=0 NormalX=0 NormalY=0 NormalZ=1 AngleXU=0 Radius=2.6 StartAngle=0.15815 EndAngle=2.98344
    g15: ArcOfCircle CenterX=11.6913 CenterY=6.75 CenterZ=0 NormalX=0 NormalY=0 NormalZ=1 AngleXU=0 Radius=2.6 StartAngle=5.39414 EndAngle=8.21943
    g16: ArcOfCircle CenterX=11.6913 CenterY=-6.75 CenterZ=0 NormalX=0 NormalY=0 NormalZ=1 AngleXU=0 Radius=2.6 StartAngle=4.34694 EndAngle=7.17223
    g17: ArcOfCircle CenterX=-5e-16 CenterY=-13.5 CenterZ=0 NormalX=0 NormalY=0 NormalZ=1 AngleXU=0 Radius=2.6 StartAngle=3.29974 EndAngle=6.12503
    g18: ArcOfCircle CenterX=-11.6913 CenterY=-6.75 CenterZ=0 NormalX=0 NormalY=0 NormalZ=1 AngleXU=0 Radius=2.6 StartAngle=2.25255 EndAngle=5.07784
    g19: ArcOfCircle CenterX=-11.6913 CenterY=6.75 CenterZ=0 NormalX=0 NormalY=0 NormalZ=1 AngleXU=0 Radius=2.6 StartAngle=1.20535 EndAngle=4.03064
    g20: LineSegment StartX=-2.56755 StartY=13.9095 StartZ=0 EndX=-3.75 EndY=6.49519 EndZ=0
    g21: LineSegment StartX=-3.75 StartY=6.49519 StartZ=0 EndX=-10.7622 EndY=9.17831 EndZ=0
    g22: LineSegment StartX=2.56755 StartY=13.9095 StartZ=0 EndX=3.75 EndY=6.49519 EndZ=0
    g23: LineSegment StartX=3.75 StartY=6.49519 StartZ=0 EndX=10.7622 EndY=9.17831 EndZ=0
    g24: LineSegment StartX=13.3297 StartY=4.73117 StartZ=0 EndX=7.5 EndY=0 EndZ=0
    g25: LineSegment StartX=7.5 StartY=0 StartZ=0 EndX=13.3297 EndY=-4.73117 EndZ=0
    g26: LineSegment StartX=10.7622 StartY=-9.17831 StartZ=0 EndX=3.75 EndY=-6.49519 EndZ=0
    g27: LineSegment StartX=3.75 StartY=-6.49519 StartZ=0 EndX=2.56755 EndY=-13.9095 EndZ=0
    g28: LineSegment StartX=-2.56755 StartY=-13.9095 StartZ=0 EndX=-3.75 EndY=-6.49519 EndZ=0
    g29: LineSegment StartX=-3.75 StartY=-6.49519 StartZ=0 EndX=-10.7622 EndY=-9.17831 EndZ=0
    g30: LineSegment StartX=-13.3297 StartY=-4.73117 StartZ=0 EndX=-7.5 EndY=9e-16 EndZ=0
    g31: LineSegment StartX=-7.5 StartY=9e-16 StartZ=0 EndX=-13.3297 EndY=4.73117 EndZ=0
  constraints (68):
    c: Coincident(g0,g1)
    c: Coincident(g1,g2)
    c: Coincident(g2,g3)
    c: Coincident(g3,g4)
    c: Coincident(g4,g5)
    c: Coincident(g5,g0)
    c: Equal(g0, g1-g5) x5
    c: PointOnObject(g0,g6)
    c: PointOnObject(g1,g6)
    c: PointOnObject(g2,g6)
    c: PointOnObject(g3,g6)
    c: PointOnObject(g4,g6)
    c: PointOnObject(g5,g6)
    c: Coincident(g6,g-1)
    c: Coincident(g7,g8)
    c: Coincident(g8,g9)
    c: Coincident(g9,g10)
    c: Coincident(g10,g11)
    c: Coincident(g11,g12)
    c: Coincident(g12,g7)
    c: Equal(g7, g8-g12) x5
    c: PointOnObject(g7,g13)
    c: PointOnObject(g8,g13)
    c: PointOnObject(g9,g13)
    c: PointOnObject(g10,g13)
    c: PointOnObject(g11,g13)
    c: PointOnObject(g12,g13)
    c: Coincident(g13,g-1)
    c: Horizontal(g0)
    c: Vertical(g8)
    c: Radius(g6) = 7.5
    c: Radius(g13) = 13.5
    c: Coincident(g14,g7)
    c: Coincident(g15,g11)
    c: Coincident(g16,g10)
    c: Coincident(g17,g9)
    c: Coincident(g18,g8)
    c: Coincident(g19,g7)
    c: Coincident(g20,g0)
    c: Coincident(g21,g20)
    c: Coincident(g22,g0)
    c: Coincident(g23,g22)
    c: Coincident(g24,g4)
    c: Coincident(g25,g24)
    c: Coincident(g26,g3)
    c: Coincident(g27,g26)
    c: Coincident(g28,g2)
    c: Coincident(g29,g28)
    c: Coincident(g31,g30)
    c: Tangent(g21,g19) = -1.5708
    c: Tangent(g20,g14) = -1.5708
    c: Tangent(g22,g14) = 1.5708
    c: Tangent(g23,g15) = 1.5708
    c: Tangent(g24,g15) = 1.5708
    c: Tangent(g25,g16) = 1.5708
    c: Tangent(g26,g16) = 1.5708
    c: Tangent(g27,g17) = 1.5708
    c: Tangent(g28,g17) = 1.5708
    c: Tangent(g29,g18) = 1.5708
    c: Tangent(g30,g18) = 1.5708
    c: Tangent(g31,g19) = 1.5708
    c: Radius(g14) = 2.6
    c: Equal(g14,g15)
    c: Equal(g15,g16)
    c: Equal(g16,g17)
    c: Equal(g17,g18)
    c: Equal(g18,g19)
    c: Coincident(g30,g1)
FEATURE [PartDesign::Pocket] Pocket561  label="Servohorn012"
  BaseFeature = -> Pocket553
  Length = 2
  Length2 = 100
  Profile = -> Sketch1260
  Type = 0
FEATURE [Sketcher::SketchObject] Sketch1429
  MapMode = 5
  Support = -> [XY_Plane421]
FEATURE [Sketcher::SketchObject] Sketch1431
  MapMode = 5
  Support = -> [XY_Plane524]
  sketch-geometry (2):
    g0: Circle CenterX=0 CenterY=0 CenterZ=0 NormalX=0 NormalY=0 NormalZ=1 AngleXU=0 Radius=2.5
    g1: Circle CenterX=0 CenterY=0 CenterZ=0 NormalX=0 NormalY=0 NormalZ=1 AngleXU=0 Radius=1
  constraints (4):
    c: Coincident(g0,g-1)
    c: Coincident(g1,g0)
    c: Radius(g0) = 2.5
    c: Radius(g1) = 1
FEATURE [PartDesign::Pad] Pad608  label="Ball Bearing Pin005"
  Length = 5
  Length2 = 100
  Profile = -> Sketch1431
  Type = 0
FEATURE [PartDesign::Chamfer] Chamfer227  label="Smooth Pinhead004"
  Base = -> Pad608 [Edge3]
  BaseFeature = -> Pad608
  Size = 0.4
FEATURE [PartDesign::Body] Body354  label="Shoulder_Joint_Ball_Bearing_Pin005"
  Group = -> [Sketch1431,Pad608,Chamfer227]
  Origin = -> Origin520
  Placement = pos=(-21.75,10,15) rot=(0,-1,0;1.5708rad)
  Tip = -> Chamfer227
FEATURE [Sketcher::SketchObject] Sketch1432
  MapMode = 5
  Placement = pos=(0,-28.25,0) rot=(1,0,0;1.5708rad)
  Support = -> [Pocket551]
  sketch-geometry (8):
    g0: LineSegment StartX=3.75 StartY=22.9 StartZ=0 EndX=6.75 EndY=22.9 EndZ=0
    g1: LineSegment StartX=6.75 StartY=22.9 StartZ=0 EndX=6.75 EndY=17.1 EndZ=0
    g2: LineSegment StartX=6.75 StartY=17.1 StartZ=0 EndX=3.75 EndY=17.1 EndZ=0
    g3: LineSegment StartX=3.75 StartY=17.1 StartZ=0 EndX=3.75 EndY=22.9 EndZ=0
    g4: LineSegment StartX=3.75 StartY=12.9 StartZ=0 EndX=6.75 EndY=12.9 EndZ=0
    g5: LineSegment StartX=6.75 StartY=12.9 StartZ=0 EndX=6.75 EndY=7.1 EndZ=0
    g6: LineSegment StartX=6.75 StartY=7.1 StartZ=0 EndX=3.75 EndY=7.1 EndZ=0
    g7: LineSegment StartX=3.75 StartY=7.1 StartZ=0 EndX=3.75 EndY=12.9 EndZ=0
  constraints (24):
    c: Coincident(g0,g1)
    c: Coincident(g1,g2)
    c: Coincident(g2,g3)
    c: Coincident(g3,g0)
    c: Horizontal(g0)
    c: Horizontal(g2)
    c: Vertical(g1)
    c: Vertical(g3)
    c: Coincident(g4,g5)
    c: Coincident(g5,g6)
    c: Coincident(g6,g7)
    c: Coincident(g7,g4)
    c: Horizontal(g4)
    c: Horizontal(g6)
    c: Vertical(g5)
    c: Vertical(g7)
    c: Equal(g0,g4)
    c: Equal(g1,g5)
    c: DistanceY(g1,g1) = 5.8
    c: DistanceY(g4,g1) = 4.2
    c: DistanceX(g-1,g5) = 6.75
    c: DistanceX(g0,g0) = 3
    c: Vertical(g4,g1)
    c: DistanceY(g-1,g5) = 7.1
FEATURE [PartDesign::Pocket] Pocket552  label="Nutholes Servo Pocket002"
  BaseFeature = -> Pocket551
  Length = 56.5
  Length2 = 100
  Profile = -> Sketch1432
  Type = 0
FEATURE [Sketcher::SketchObject] Sketch1247
  MapMode = 5
  Placement = pos=(9.75,0,0) rot=(0.57735,0.57735,0.57735;2.0944rad)
  Support = -> [Pocket552]
  sketch-geometry (4):
    g0: Circle CenterX=-24.25 CenterY=20 CenterZ=0 NormalX=0 NormalY=0 NormalZ=1 AngleXU=0 Radius=1.6
    g1: Circle CenterX=-24.25 CenterY=10 CenterZ=0 NormalX=0 NormalY=0 NormalZ=1 AngleXU=0 Radius=1.6
    g2: Circle CenterX=24.25 CenterY=20 CenterZ=0 NormalX=0 NormalY=0 NormalZ=1 AngleXU=0 Radius=1.6
    g3: Circle CenterX=24.25 CenterY=10 CenterZ=0 NormalX=0 NormalY=0 NormalZ=1 AngleXU=0 Radius=1.6
  constraints (11):
    c: Vertical(g3,g2)
    c: Vertical(g1,g0)
    c: Symmetric(g0,g2,g-2)
    c: Radius(g0) = 1.6
    c: Equal(g0,g1)
    c: Equal(g0,g2)
    c: Equal(g0,g3)
    c: DistanceY(g3,g2) = 10
    c: Horizontal(g1,g3)
    c: DistanceY(g-1,g3) = 10
    c: DistanceX(g0,g2) = 48.5
FEATURE [PartDesign::Pocket] Pocket547  label="Screwholes Servo Pocket002"
  BaseFeature = -> Pocket552
  Length = 18
  Length2 = 100
  Profile = -> Sketch1247
  Type = 0
FEATURE [Sketcher::SketchObject] Sketch1261
  MapMode = 5
  Placement = pos=(-18.75,0,0) rot=(0.57735,0.57735,0.57735;2.0944rad)
  Support = -> [Pocket547]
  sketch-geometry (1):
    g0: Circle CenterX=10 CenterY=15 CenterZ=0 NormalX=0 NormalY=0 NormalZ=1 AngleXU=0 Radius=0.95
  constraints (3):
    c: DistanceY(g-1,g0) = 15
    c: DistanceX(g-1,g0) = 10
    c: Radius(g0) = 0.95
FEATURE [PartDesign::Pocket] Pocket555  label="Screwhole Ball Bearing Pin002"
  BaseFeature = -> Pocket547
  Length = 3
  Length2 = 100
  Profile = -> Sketch1261
  Type = 0
FEATURE [Sketcher::SketchObject] Sketch1245
  MapMode = 5
  Placement = pos=(-18.75,0,0) rot=(0.57735,0.57735,0.57735;2.0944rad)
  Support = -> [Pocket555]
  sketch-geometry (7):
    g0: LineSegment StartX=12.05 StartY=13.8164 StartZ=0 EndX=12.05 EndY=16.1836 EndZ=0
    g1: LineSegment StartX=12.05 StartY=16.1836 StartZ=0 EndX=10 EndY=17.3671 EndZ=0
    g2: LineSegment StartX=10 StartY=17.3671 StartZ=0 EndX=7.95 EndY=16.1836 EndZ=0
    g3: LineSegment StartX=7.95 StartY=16.1836 StartZ=0 EndX=7.95 EndY=13.8164 EndZ=0
    g4: LineSegment StartX=7.95 StartY=13.8164 StartZ=0 EndX=10 EndY=12.6329 EndZ=0
    g5: LineSegment StartX=10 StartY=12.6329 StartZ=0 EndX=12.05 EndY=13.8164 EndZ=0
    g6: Circle [constr] CenterX=10 CenterY=15 CenterZ=0 NormalX=0 NormalY=0 NormalZ=1 AngleXU=0 Radius=2.36714
  constraints (17):
    c: Coincident(g0,g1)
    c: Coincident(g1,g2)
    c: Coincident(g2,g3)
    c: Coincident(g3,g4)
    c: Coincident(g4,g5)
    c: Coincident(g5,g0)
    c: Equal(g0, g1-g5) x5
    c: PointOnObject(g0,g6)
    c: PointOnObject(g1,g6)
    c: PointOnObject(g2,g6)
    c: PointOnObject(g3,g6)
    c: PointOnObject(g4,g6)
    c: PointOnObject(g5,g6)
    c: Vertical(g3)
    c: DistanceX(g-1,g6) = 10
    c: DistanceY(g-1,g6) = 15
    c: Distance(g0,g4) = 4.1
FEATURE [PartDesign::Pocket] Pocket563  label="Nuthole Ball Bearing Pin002"
  BaseFeature = -> Pocket555
  Length = 1.5
  Length2 = 100
  Profile = -> Sketch1245
  Type = 0
FEATURE [Sketcher::SketchObject] Sketch1430
  MapMode = 5
  Placement = pos=(0,28.25,0) rot=(0,0.707107,0.707107;3.14159rad)
  Support = -> [Pocket563]
  sketch-geometry (4):
    g0: LineSegment StartX=9.25 StartY=25 StartZ=0 EndX=14.25 EndY=25 EndZ=0
    g1: LineSegment StartX=14.25 StartY=25 StartZ=0 EndX=14.25 EndY=11.5 EndZ=0
    g2: ArcOfCircle CenterX=11.75 CenterY=11.5 CenterZ=0 NormalX=0 NormalY=0 NormalZ=1 AngleXU=0 Radius=2.5 StartAngle=3.14159 EndAngle=6.28319
    g3: LineSegment StartX=9.25 StartY=11.5 StartZ=0 EndX=9.25 EndY=25 EndZ=0
  constraints (11):
    c: Horizontal(g0)
    c: Coincident(g0,g1)
    c: Vertical(g1)
    c: Tangent(g1,g2) = 1.5708
    c: Tangent(g2,g3) = 1.5708
    c: Coincident(g3,g0)
    c: DistanceX(g0,g0) = 5
    c: Vertical(g3)
    c: DistanceX(g-1,g2) = 11.75
    c: DistanceY(g-1,g2) = 11.5
    c: DistanceY(g1,g1) = 13.5
FEATURE [PartDesign::Pocket] Pocket545  label="Servocable010"
  BaseFeature = -> Pocket563
  Length = 8
  Length2 = 100
  Profile = -> Sketch1430
  Type = 0
FEATURE [Sketcher::SketchObject] Sketch1433
  MapMode = 5
  Placement = pos=(0,0,0) rot=(1,0,0;3.14159rad)
  Support = -> [Pad599]
  sketch-geometry (7):
    g0: LineSegment StartX=1.275 StartY=0.736122 StartZ=0 EndX=0 EndY=1.47224 EndZ=0
    g1: LineSegment StartX=0 StartY=1.47224 StartZ=0 EndX=-1.275 EndY=0.736122 EndZ=0
    g2: LineSegment StartX=-1.275 StartY=0.736122 StartZ=0 EndX=-1.275 EndY=-0.736122 EndZ=0
    g3: LineSegment StartX=-1.275 StartY=-0.736122 StartZ=0 EndX=1.34766e-11 EndY=-1.47224 EndZ=0
    g4: LineSegment StartX=1.34766e-11 StartY=-1.47224 StartZ=0 EndX=1.275 EndY=-0.736122 EndZ=0
    g5: LineSegment StartX=1.275 StartY=-0.736122 StartZ=0 EndX=1.275 EndY=0.736122 EndZ=0
    g6: Circle [constr] CenterX=0 CenterY=0 CenterZ=0 NormalX=0 NormalY=0 NormalZ=1 AngleXU=0 Radius=1.47224
  constraints (16):
    c: Coincident(g0,g1)
    c: Coincident(g1,g2)
    c: Coincident(g2,g3)
    c: Coincident(g3,g4)
    c: Coincident(g4,g5)
    c: Coincident(g5,g0)
    c: Equal(g0, g1-g5) x5
    c: PointOnObject(g0,g6)
    c: PointOnObject(g1,g6)
    c: PointOnObject(g2,g6)
    c: PointOnObject(g3,g6)
    c: PointOnObject(g4,g6)
    c: PointOnObject(g5,g6)
    c: Coincident(g6,g-1)
    c: PointOnObject(g0,g-2)
    c: DistanceX(g1,g0) = 2.55
FEATURE [PartDesign::Pocket] Pocket520  label="M3x20 Wrench049"
  BaseFeature = -> Pad599
  Length = 1.3
  Length2 = 100
  Profile = -> Sketch1433
  Type = 0
FEATURE [PartDesign::Chamfer] Chamfer258  label="M3x20 Smooth046"
  Base = -> Pocket520 [Face11,Edge2,Edge24,Edge3]
  BaseFeature = -> Pocket520
  Size = 0.2
FEATURE [PartDesign::Body] Body341  label="M3x071"
  Group = -> [Sketch1426,Pad601,Sketch1414,Pad599,Sketch1433,Pocket520,Chamfer258]
  Origin = -> Origin526
  Placement = pos=(-115.35,28,62.05) rot=(1,0,0;1.5708rad)
  Tip = -> Chamfer258
FEATURE [Sketcher::SketchObject] Sketch1436
  MapMode = 5
  Placement = pos=(0,0,0) rot=(1,0,0;1.5708rad)
  Support = -> [XZ_Plane492]
  sketch-geometry (4):
    g0: LineSegment StartX=68.5 StartY=25 StartZ=0 EndX=125 EndY=25 EndZ=0
    g1: LineSegment StartX=125 StartY=25 StartZ=0 EndX=125 EndY=5 EndZ=0
    g2: LineSegment StartX=125 StartY=5 StartZ=0 EndX=68.5 EndY=5 EndZ=0
    g3: LineSegment StartX=68.5 StartY=5 StartZ=0 EndX=68.5 EndY=25 EndZ=0
  constraints (12):
    c: Coincident(g0,g1)
    c: Coincident(g1,g2)
    c: Coincident(g2,g3)
    c: Coincident(g3,g0)
    c: Horizontal(g0)
    c: Horizontal(g2)
    c: Vertical(g1)
    c: Vertical(g3)
    c: DistanceX(g0,g0) = 56.5
    c: DistanceY(g3,g3) = 20
    c: DistanceY(g-1,g2) = 5
    c: DistanceX(g-1,g0) = 68.5
FEATURE [Sketcher::SketchObject] Sketch1437
  MapMode = 5
  Support = -> [XY_Plane493]
  sketch-geometry (12):
    g0: LineSegment StartX=0 StartY=0 StartZ=0 EndX=0 EndY=57 EndZ=0
    g1: LineSegment StartX=0 StartY=57 StartZ=0 EndX=40 EndY=57 EndZ=0
    g2: ArcOfCircle CenterX=40 CenterY=44.5 CenterZ=0 NormalX=0 NormalY=0 NormalZ=1 AngleXU=0 Radius=12.5 StartAngle=0.643501 EndAngle=1.5708
    g3: ArcOfCircle CenterX=60 CenterY=59.5 CenterZ=0 NormalX=0 NormalY=0 NormalZ=1 AngleXU=0 Radius=12.5 StartAngle=3.78509 EndAngle=4.71239
    g4: LineSegment StartX=60 StartY=47 StartZ=0 EndX=120 EndY=47 EndZ=0
    g5: ArcOfCircle CenterX=120 CenterY=37 CenterZ=0 NormalX=0 NormalY=0 NormalZ=1 AngleXU=0 Radius=10 StartAngle=2e-16 EndAngle=1.5708
    g6: LineSegment StartX=130 StartY=37 StartZ=0 EndX=130 EndY=15 EndZ=0
    g7: ArcOfCircle CenterX=125 CenterY=15 CenterZ=0 NormalX=0 NormalY=0 NormalZ=1 AngleXU=0 Radius=5 StartAngle=4.71239 EndAngle=6.28319
    g8: LineSegment StartX=125 StartY=10 StartZ=0 EndX=60 EndY=10 EndZ=0
    g9: LineSegment StartX=40 StartY=0 StartZ=0 EndX=0 EndY=0 EndZ=0
    g10: ArcOfCircle CenterX=40 CenterY=12.5 CenterZ=0 NormalX=0 NormalY=0 NormalZ=1 AngleXU=0 Radius=12.5 StartAngle=4.71239 EndAngle=5.63968
    g11: ArcOfCircle CenterX=60 CenterY=-2.5 CenterZ=0 NormalX=0 NormalY=0 NormalZ=1 AngleXU=0 Radius=12.5 StartAngle=1.5708 EndAngle=2.49809
  constraints (31):
    c: Coincident(g-1,g0)
    c: PointOnObject(g0,g-2)
    c: Coincident(g0,g1)
    c: Horizontal(g1)
    c: Tangent(g1,g2) = 1.5708
    c: Tangent(g2,g3) = 1.5708
    c: Tangent(g3,g4) = -1.5708
    c: Tangent(g4,g5) = 1.5708
    c: Tangent(g5,g6) = 1.5708
    c: Tangent(g6,g7) = 1.5708
    c: Tangent(g7,g8) = 1.5708
    c: Coincident(g9,g0)
    c: Horizontal(g9)
    c: Horizontal(g4)
    c: Horizontal(g8)
    c: Vertical(g6)
    c: Tangent(g11,g8) = -1.5708
    c: Tangent(g11,g10) = 1.5708
    c: Radius(g7) = 5
    c: Radius(g5) = 10
    c: DistanceX(g1,g1) = 40
    c: DistanceX(g0,g6) = 130
    c: DistanceX(g1,g3) = 20
    c: Tangent(g10,g9) = 1.5708
    c: DistanceX(g9,g8) = 20
    c: DistanceX(g9,g9) = 40
    c: DistanceY(g0,g0) = 57
    c: DistanceY(g9,g8) = 10
    c: DistanceY(g3,g1) = 10
    c: DistanceX(g10,g8) = 10
    c: DistanceX(g2,g3) = 10
FEATURE [PartDesign::Pad] Pad481  label="Baseplate022"
  Length = 30
  Length2 = 100
  Profile = -> Sketch1437
  Type = 0
FEATURE [PartDesign::Pocket] Pocket438  label="Servohorn Mount Pocket005"
  BaseFeature = -> Pad481
  Length = 5
  Length2 = 100
  Profile = -> Pad481 [Face12]
  Type = 0
FEATURE [PartDesign::Pocket] Pocket445  label="Ball Bearing Mount Pocket004"
  BaseFeature = -> Pocket438
  Length = 5
  Length2 = 100
  Profile = -> Pocket438 [Face3]
  Type = 0
FEATURE [Sketcher::SketchObject] Sketch1332
  MapMode = 5
  Placement = pos=(40,0,0) rot=(0.57735,-0.57735,-0.57735;2.0944rad)
  Support = -> [Pocket445]
  sketch-geometry (6):
    g0: ArcOfCircle CenterX=-25.9999 CenterY=20 CenterZ=0 NormalX=0 NormalY=0 NormalZ=1 AngleXU=0 Radius=25.9999 StartAngle=6.28318 EndAngle=6.67798
    g1: LineSegment StartX=-2 StartY=30 StartZ=0 EndX=1 EndY=30 EndZ=0
    g2: LineSegment StartX=1 StartY=30 StartZ=0 EndX=1 EndY=0 EndZ=0
    g3: LineSegment StartX=1 StartY=0 StartZ=0 EndX=-2 EndY=2.39524e-11 EndZ=0
    g4: ArcOfCircle CenterX=-25.9999 CenterY=9.99999 CenterZ=0 NormalX=0 NormalY=0 NormalZ=1 AngleXU=0 Radius=25.9999 StartAngle=5.88839 EndAngle=6.28319
    g5: LineSegment StartX=-2.5011e-12 StartY=10 StartZ=0 EndX=-2.5011e-12 EndY=20 EndZ=0
  constraints (20):
    c: DistanceY(g0,g0) = 10
    c: DistanceX(g0,g-1) = 2
    c: Vertical(g0,g-1)
    c: Tangent(g0,g-2)
    c: DistanceY(g-1,g0) = 30
    c: Coincident(g0,g1)
    c: Coincident(g1,g2)
    c: PointOnObject(g2,g-1)
    c: Vertical(g2)
    c: Coincident(g2,g3)
    c: PointOnObject(g3,g-1)
    c: Coincident(g4,g3)
    c: Tangent(g4,g-2)
    c: Vertical(g3,g0)
    c: DistanceY(g-1,g4) = 10
    c: Coincident(g5,g4)
    c: Coincident(g5,g0)
    c: Vertical(g5)
    c: Horizontal(g1)
    c: DistanceX(g1,g1) = 3
FEATURE [PartDesign::SubtractivePipe] SubtractivePipe014  label="Smooth Beveled Surfaces005"
  AuxilleryCurvelinear = true
  AuxillerySpineTangent = false
  BaseFeature = -> Pocket445
  Binormal = (0,0,0)
  Mode = 0
  Profile = -> Sketch1332
  Spine = -> Pocket445 [Edge21,Edge22,Edge23,Edge24,Edge25,Edge26,Edge27,Edge28,Edge29]
  SpineTangent = false
  Transformation = 0
  Transition = 0
FEATURE [PartDesign::Fillet] Fillet167  label="Smooth Edges012"
  Base = -> SubtractivePipe014 [Edge20,Edge5]
  BaseFeature = -> SubtractivePipe014
  Radius = 1.5
FEATURE [Sketcher::SketchObject] Sketch1435
  MapMode = 5
  Placement = pos=(0,5,0) rot=(1,0,0;1.5708rad)
  Support = -> [Fillet167]
  sketch-geometry (1):
    g0: Circle CenterX=0 CenterY=0 CenterZ=0 NormalX=0 NormalY=0 NormalZ=1 AngleXU=0 Radius=30
  constraints (2):
    c: Coincident(g0,g-1)
    c: Radius(g0) = 30
FEATURE [PartDesign::Pocket] Pocket435  label="Joint Pan004"
  BaseFeature = -> Fillet167
  Length = 47
  Length2 = 100
  Profile = -> Sketch1435
  Type = 0
FEATURE [Sketcher::SketchObject] Sketch1438
  MapMode = 5
  Support = -> [XY_Plane510]
  sketch-geometry (8):
    g0: LineSegment StartX=0 StartY=3.17543 StartZ=0 EndX=-2.75 EndY=1.58771 EndZ=0
    g1: LineSegment StartX=-2.75 StartY=1.58771 StartZ=0 EndX=-2.75 EndY=-1.58771 EndZ=0
    g2: LineSegment StartX=-2.75 StartY=-1.58771 StartZ=0 EndX=0 EndY=-3.17543 EndZ=0
    g3: LineSegment StartX=0 StartY=-3.17543 StartZ=0 EndX=2.75 EndY=-1.58771 EndZ=0
    g4: LineSegment StartX=2.75 StartY=-1.58771 StartZ=0 EndX=2.75 EndY=1.58771 EndZ=0
    g5: LineSegment StartX=2.75 StartY=1.58771 StartZ=0 EndX=0 EndY=3.17543 EndZ=0
    g6: Circle [constr] CenterX=0 CenterY=0 CenterZ=0 NormalX=0 NormalY=0 NormalZ=1 AngleXU=0 Radius=3.17543
    g7: Circle CenterX=0 CenterY=0 CenterZ=0 NormalX=0 NormalY=0 NormalZ=1 AngleXU=0 Radius=1.5
  constraints (18):
    c: Coincident(g0,g1)
    c: Coincident(g1,g2)
    c: Coincident(g2,g3)
    c: Coincident(g3,g4)
    c: Coincident(g4,g5)
    c: Coincident(g5,g0)
    c: Equal(g0, g1-g5) x5
    c: PointOnObject(g0,g6)
    c: PointOnObject(g1,g6)
    c: PointOnObject(g2,g6)
    c: PointOnObject(g3,g6)
    c: PointOnObject(g4,g6)
    c: PointOnObject(g5,g6)
    c: Coincident(g6,g-1)
    c: PointOnObject(g5,g-2)
    c: DistanceX(g0,g4) = 5.5
    c: Coincident(g7,g-1)
    c: Radius(g7) = 1.5
FEATURE [PartDesign::Pad] Pad576  label="M3 Nut Primitive112"
  Length = 1.2
  Length2 = 1.2
  Profile = -> Sketch1438
  Type = 4
FEATURE [Sketcher::SketchObject] Sketch1372
  ExternalGeometry = -> [Pad576]
  MapMode = 5
  Placement = pos=(0,0,0) rot=(0.57735,0.57735,0.57735;2.0944rad)
  Support = -> [YZ_Plane491]
  sketch-geometry (6):
    g0: LineSegment StartX=-2.67543 StartY=1.2 StartZ=0 EndX=-3.67543 EndY=1.2 EndZ=0
    g1: LineSegment StartX=-3.67543 StartY=1.2 StartZ=0 EndX=-3.67543 EndY=-1.2 EndZ=0
    g2: LineSegment StartX=-3.67543 StartY=-1.2 StartZ=0 EndX=-2.67543 EndY=-1.2 EndZ=0
    g3: LineSegment StartX=-2.67543 StartY=-1.2 StartZ=0 EndX=-3.17543 EndY=-1 EndZ=0
    g4: LineSegment StartX=-3.17543 StartY=-1 StartZ=0 EndX=-3.17543 EndY=1 EndZ=0
    g5: LineSegment StartX=-3.17543 StartY=1 StartZ=0 EndX=-2.67543 EndY=1.2 EndZ=0
  constraints (15):
    c: Horizontal(g0)
    c: Coincident(g0,g1)
    c: Coincident(g1,g2)
    c: Coincident(g2,g3)
    c: Coincident(g3,g4)
    c: Coincident(g4,g5)
    c: Coincident(g5,g0)
    c: Symmetric(g4,g3,g-1)
    c: Symmetric(g0,g2,g-1)
    c: Symmetric(g1,g0,g-1)
    c: DistanceX(g0,g4) = 0.5
    c: DistanceY(g3,g4) = 2
    c: DistanceY(g1,g0) = 2.4
    c: PointOnObject(g3,g-3)
    c: DistanceX(g4,g0) = 0.5
FEATURE [PartDesign::Groove] Groove097  label="M3 Nut Smooth093"
  Angle = 360
  Axis = (-2e-16,3e-16,1)
  Base = (0,0,0)
  BaseFeature = -> Pad576
  Profile = -> Sketch1372
  ReferenceAxis = -> Sketch1372 [V_Axis]
  Reversed = true
FEATURE [PartDesign::Chamfer] Chamfer257  label="M3 Nut Smooth Hole109"
  Base = -> Groove097 [Edge24,Edge23]
  BaseFeature = -> Groove097
  Size = 0.2
FEATURE [PartDesign::Body] Body308  label="M3 Nut053"
  Group = -> [Sketch1438,Pad576,Sketch1372,Groove097,Chamfer257]
  Origin = -> Origin495
  Placement = pos=(-115.35,7.7,62.05) rot=(0.57735,0.57735,-0.57735;2.0944rad)
  Tip = -> Chamfer257
FEATURE [Sketcher::SketchObject] Sketch1439
  MapMode = 5
  Placement = pos=(40,0,0) rot=(0.57735,-0.57735,-0.57735;2.0944rad)
  Support = -> [Pocket449]
  sketch-geometry (6):
    g0: ArcOfCircle CenterX=-25.9999 CenterY=20 CenterZ=0 NormalX=0 NormalY=0 NormalZ=1 AngleXU=0 Radius=25.9999 StartAngle=6.28318 EndAngle=6.67798
    g1: LineSegment StartX=-2 StartY=30 StartZ=0 EndX=1 EndY=30 EndZ=0
    g2: LineSegment StartX=1 StartY=30 StartZ=0 EndX=1 EndY=0 EndZ=0
    g3: LineSegment StartX=1 StartY=0 StartZ=0 EndX=-2 EndY=2.39524e-11 EndZ=0
    g4: ArcOfCircle CenterX=-25.9999 CenterY=9.99999 CenterZ=0 NormalX=0 NormalY=0 NormalZ=1 AngleXU=0 Radius=25.9999 StartAngle=5.88839 EndAngle=6.28319
    g5: LineSegment StartX=-2.5011e-12 StartY=10 StartZ=0 EndX=-2.5011e-12 EndY=20 EndZ=0
  constraints (20):
    c: DistanceY(g0,g0) = 10
    c: DistanceX(g0,g-1) = 2
    c: Vertical(g0,g-1)
    c: Tangent(g0,g-2)
    c: DistanceY(g-1,g0) = 30
    c: Coincident(g0,g1)
    c: Coincident(g1,g2)
    c: PointOnObject(g2,g-1)
    c: Vertical(g2)
    c: Coincident(g2,g3)
    c: PointOnObject(g3,g-1)
    c: Coincident(g4,g3)
    c: Tangent(g4,g-2)
    c: Vertical(g3,g0)
    c: DistanceY(g-1,g4) = 10
    c: Coincident(g5,g4)
    c: Coincident(g5,g0)
    c: Vertical(g5)
    c: Horizontal(g1)
    c: DistanceX(g1,g1) = 3
FEATURE [PartDesign::SubtractivePipe] SubtractivePipe013  label="Smooth Beveled Surfaces004"
  AuxilleryCurvelinear = true
  AuxillerySpineTangent = false
  BaseFeature = -> Pocket449
  Binormal = (0,0,0)
  Mode = 0
  Profile = -> Sketch1439
  Spine = -> Pocket449 [Edge21,Edge22,Edge23,Edge24,Edge25,Edge26,Edge27,Edge28,Edge29]
  SpineTangent = false
  Transformation = 0
  Transition = 0
FEATURE [Sketcher::SketchObject] Sketch1444
  MapMode = 5
  Placement = pos=(0,0,0) rot=(0.57735,0.57735,0.57735;2.0944rad)
  Support = -> [YZ_Plane493]
  sketch-geometry (4):
    g0: LineSegment StartX=35.5 StartY=17.1 StartZ=0 EndX=38.5 EndY=17.1 EndZ=0
    g1: LineSegment StartX=38.5 StartY=17.1 StartZ=0 EndX=38.5 EndY=22.9 EndZ=0
    g2: LineSegment StartX=38.5 StartY=22.9 StartZ=0 EndX=35.5 EndY=22.9 EndZ=0
    g3: LineSegment StartX=35.5 StartY=22.9 StartZ=0 EndX=35.5 EndY=17.1 EndZ=0
  constraints (12):
    c: Coincident(g0,g1)
    c: Coincident(g1,g2)
    c: Coincident(g2,g3)
    c: Coincident(g3,g0)
    c: Horizontal(g0)
    c: Horizontal(g2)
    c: Vertical(g1)
    c: Vertical(g3)
    c: DistanceX(g2,g2) = 3
    c: DistanceY(g1,g1) = 5.8
    c: DistanceX(g-1,g0) = 38.5
    c: DistanceY(g-1,g0) = 17.1
FEATURE [Sketcher::SketchObject] Sketch1446
  MapMode = 5
  Placement = pos=(0,0,0) rot=(1,0,0;1.5708rad)
  Support = -> [XZ_Plane494]
  sketch-geometry (4):
    g0: LineSegment StartX=68.5 StartY=25 StartZ=0 EndX=125 EndY=25 EndZ=0
    g1: LineSegment StartX=125 StartY=25 StartZ=0 EndX=125 EndY=5 EndZ=0
    g2: LineSegment StartX=125 StartY=5 StartZ=0 EndX=68.5 EndY=5 EndZ=0
    g3: LineSegment StartX=68.5 StartY=5 StartZ=0 EndX=68.5 EndY=25 EndZ=0
  constraints (12):
    c: Coincident(g0,g1)
    c: Coincident(g1,g2)
    c: Coincident(g2,g3)
    c: Coincident(g3,g0)
    c: Horizontal(g0)
    c: Horizontal(g2)
    c: Vertical(g1)
    c: Vertical(g3)
    c: DistanceX(g0,g0) = 56.5
    c: DistanceY(g3,g3) = 20
    c: DistanceY(g-1,g2) = 5
    c: DistanceX(g-1,g0) = 68.5
FEATURE [Sketcher::SketchObject] Sketch1447
  MapMode = 5
  Support = -> [XY_Plane488]
  sketch-geometry (1):
    g0: Circle CenterX=0 CenterY=0 CenterZ=0 NormalX=0 NormalY=0 NormalZ=1 AngleXU=0 Radius=8
  constraints (2):
    c: Coincident(g0,g-1)
    c: Radius(g0) = 8
FEATURE [PartDesign::Pad] Pad495
  Length = 5
  Length2 = 100
  Profile = -> Sketch1447
  Type = 0
FEATURE [Sketcher::SketchObject] Sketch1448
  ExternalGeometry = -> [Pocket435]
  MapMode = 5
  Placement = pos=(0,5,0) rot=(1,0,0;1.5708rad)
  Support = -> [Pocket435]
  sketch-geometry (7):
    g0: ArcOfCircle CenterX=23.5 CenterY=28.2018 CenterZ=0 NormalX=0 NormalY=0 NormalZ=1 AngleXU=0 Radius=1.79818 StartAngle=1.57079 EndAngle=2.66896
    g1: LineSegment StartX=21.8989 StartY=29.0204 StartZ=0 EndX=19.5977 EndY=24.5195 EndZ=0
    g2: ArcOfCircle CenterX=21.1988 CenterY=23.701 CenterZ=0 NormalX=0 NormalY=0 NormalZ=1 AngleXU=0 Radius=1.79818 StartAngle=2.66896 EndAngle=3.98266
    g3: Circle [constr] CenterX=0 CenterY=0 CenterZ=0 NormalX=0 NormalY=0 NormalZ=1 AngleXU=0 Radius=30
    g4: LineSegment StartX=23.5 StartY=30 StartZ=0 EndX=0 EndY=30 EndZ=0
    g5: LineSegment StartX=0 StartY=30 StartZ=0 EndX=0 EndY=22.3607 EndZ=0
    g6: LineSegment StartX=0 StartY=22.3607 StartZ=0 EndX=20 EndY=22.3607 EndZ=0
  constraints (19):
    c: Coincident(g3,g-1)
    c: Radius(g3) = 30
    c: Coincident(g4,g0)
    c: PointOnObject(g4,g3)
    c: Horizontal(g4)
    c: Tangent(g4,g0)
    c: Coincident(g5,g4)
    c: Vertical(g5)
    c: Tangent(g2,g3) = 1.5708
    c: Tangent(g2,g1) = -1.5708
    c: Tangent(g1,g0) = -1.5708
    c: DistanceX(g4,g4) = 23.5
    c: PointOnObject(g4,g-2)
    c: DistanceX(g5,g2) = 20
    c: Equal(g0,g2)
    c: Coincident(g6,g5)
    c: Coincident(g6,g2)
    c: Horizontal(g6)
    c: Horizontal(g-3,g0)
FEATURE [PartDesign::Pocket] Pocket448  label="Shortened Angled Top005"
  BaseFeature = -> Pocket435
  Length = 47
  Length2 = 100
  Profile = -> Sketch1448
  Type = 0
FEATURE [PartDesign::Pocket] Pocket444  label="Servoplacement Helper Pocket005"
  BaseFeature = -> Pocket448
  Length = 15
  Length2 = 100
  Profile = -> Sketch1446
  Type = 0
FEATURE [PartDesign::Pad] Pad478  label="Servoplacement Helper Pad005"
  BaseFeature = -> Pocket444
  Length = 5
  Length2 = 100
  Profile = -> Pocket444 [Face60]
  Type = 0
FEATURE [PartDesign::Fillet] Fillet168  label="Servoplacement Smooth Edges004"
  Base = -> Pad478 [Edge121,Edge125]
  BaseFeature = -> Pad478
  Radius = 0.4
FEATURE [Sketcher::SketchObject] Sketch1450
  MapMode = 5
  Support = -> [XY_Plane506]
  sketch-geometry (8):
    g0: LineSegment StartX=0 StartY=3.17543 StartZ=0 EndX=-2.75 EndY=1.58771 EndZ=0
    g1: LineSegment StartX=-2.75 StartY=1.58771 StartZ=0 EndX=-2.75 EndY=-1.58771 EndZ=0
    g2: LineSegment StartX=-2.75 StartY=-1.58771 StartZ=0 EndX=0 EndY=-3.17543 EndZ=0
    g3: LineSegment StartX=0 StartY=-3.17543 StartZ=0 EndX=2.75 EndY=-1.58771 EndZ=0
    g4: LineSegment StartX=2.75 StartY=-1.58771 StartZ=0 EndX=2.75 EndY=1.58771 EndZ=0
    g5: LineSegment StartX=2.75 StartY=1.58771 StartZ=0 EndX=0 EndY=3.17543 EndZ=0
    g6: Circle [constr] CenterX=0 CenterY=0 CenterZ=0 NormalX=0 NormalY=0 NormalZ=1 AngleXU=0 Radius=3.17543
    g7: Circle CenterX=0 CenterY=0 CenterZ=0 NormalX=0 NormalY=0 NormalZ=1 AngleXU=0 Radius=1.5
  constraints (18):
    c: Coincident(g0,g1)
    c: Coincident(g1,g2)
    c: Coincident(g2,g3)
    c: Coincident(g3,g4)
    c: Coincident(g4,g5)
    c: Coincident(g5,g0)
    c: Equal(g0, g1-g5) x5
    c: PointOnObject(g0,g6)
    c: PointOnObject(g1,g6)
    c: PointOnObject(g2,g6)
    c: PointOnObject(g3,g6)
    c: PointOnObject(g4,g6)
    c: PointOnObject(g5,g6)
    c: Coincident(g6,g-1)
    c: PointOnObject(g5,g-2)
    c: DistanceX(g0,g4) = 5.5
    c: Coincident(g7,g-1)
    c: Radius(g7) = 1.5
FEATURE [PartDesign::Pad] Pad483  label="M3 Nut Primitive092"
  Length = 1.2
  Length2 = 1.2
  Profile = -> Sketch1450
  Type = 4
FEATURE [Sketcher::SketchObject] Sketch1394
  ExternalGeometry = -> [Pad483]
  MapMode = 5
  Placement = pos=(0,0,0) rot=(0.57735,0.57735,0.57735;2.0944rad)
  Support = -> [YZ_Plane503]
  sketch-geometry (6):
    g0: LineSegment StartX=-2.67543 StartY=1.2 StartZ=0 EndX=-3.67543 EndY=1.2 EndZ=0
    g1: LineSegment StartX=-3.67543 StartY=1.2 StartZ=0 EndX=-3.67543 EndY=-1.2 EndZ=0
    g2: LineSegment StartX=-3.67543 StartY=-1.2 StartZ=0 EndX=-2.67543 EndY=-1.2 EndZ=0
    g3: LineSegment StartX=-2.67543 StartY=-1.2 StartZ=0 EndX=-3.17543 EndY=-1 EndZ=0
    g4: LineSegment StartX=-3.17543 StartY=-1 StartZ=0 EndX=-3.17543 EndY=1 EndZ=0
    g5: LineSegment StartX=-3.17543 StartY=1 StartZ=0 EndX=-2.67543 EndY=1.2 EndZ=0
  constraints (15):
    c: Horizontal(g0)
    c: Coincident(g0,g1)
    c: Coincident(g1,g2)
    c: Coincident(g2,g3)
    c: Coincident(g3,g4)
    c: Coincident(g4,g5)
    c: Coincident(g5,g0)
    c: Symmetric(g4,g3,g-1)
    c: Symmetric(g0,g2,g-1)
    c: Symmetric(g1,g0,g-1)
    c: DistanceX(g0,g4) = 0.5
    c: DistanceY(g3,g4) = 2
    c: DistanceY(g1,g0) = 2.4
    c: PointOnObject(g3,g-3)
    c: DistanceX(g4,g0) = 0.5
FEATURE [PartDesign::Groove] Groove100  label="M3 Nut Smooth096"
  Angle = 360
  Axis = (-2e-16,3e-16,1)
  Base = (0,0,0)
  BaseFeature = -> Pad483
  Profile = -> Sketch1394
  ReferenceAxis = -> Sketch1394 [V_Axis]
  Reversed = true
FEATURE [PartDesign::Chamfer] Chamfer256  label="M3 Nut Smooth Hole108"
  Base = -> Groove100 [Edge24,Edge23]
  BaseFeature = -> Groove100
  Size = 0.2
FEATURE [PartDesign::Body] Body337  label="M3 Nut060"
  Group = -> [Sketch1450,Pad483,Sketch1394,Groove100,Chamfer256]
  Origin = -> Origin460
  Placement = pos=(-110.6,-9.3,52.1) rot=(0.57735,0.57735,-0.57735;2.0944rad)
  Tip = -> Chamfer256
FEATURE [Sketcher::SketchObject] Sketch1452
  MapMode = 5
  Placement = pos=(0,0,0) rot=(0.57735,0.57735,0.57735;2.0944rad)
  Support = -> [YZ_Plane494]
  sketch-geometry (4):
    g0: LineSegment StartX=18.5 StartY=17.1 StartZ=0 EndX=21.5 EndY=17.1 EndZ=0
    g1: LineSegment StartX=21.5 StartY=17.1 StartZ=0 EndX=21.5 EndY=22.9 EndZ=0
    g2: LineSegment StartX=21.5 StartY=22.9 StartZ=0 EndX=18.5 EndY=22.9 EndZ=0
    g3: LineSegment StartX=18.5 StartY=22.9 StartZ=0 EndX=18.5 EndY=17.1 EndZ=0
  constraints (12):
    c: Coincident(g0,g1)
    c: Coincident(g1,g2)
    c: Coincident(g2,g3)
    c: Coincident(g3,g0)
    c: Horizontal(g0)
    c: Horizontal(g2)
    c: Vertical(g1)
    c: Vertical(g3)
    c: DistanceX(g2,g2) = 3
    c: DistanceY(g1,g1) = 5.8
    c: DistanceX(g-1,g0) = 21.5
    c: DistanceY(g-1,g0) = 17.1
FEATURE [Sketcher::SketchObject] Sketch1454
  MapMode = 5
  Placement = pos=(0,0,0) rot=(0.57735,0.57735,0.57735;2.0944rad)
  Support = -> [YZ_Plane494]
  sketch-geometry (4):
    g0: LineSegment StartX=18.5 StartY=7.1 StartZ=0 EndX=21.5 EndY=7.1 EndZ=0
    g1: LineSegment StartX=21.5 StartY=7.1 StartZ=0 EndX=21.5 EndY=12.9 EndZ=0
    g2: LineSegment StartX=21.5 StartY=12.9 StartZ=0 EndX=18.5 EndY=12.9 EndZ=0
    g3: LineSegment StartX=18.5 StartY=12.9 StartZ=0 EndX=18.5 EndY=7.1 EndZ=0
  constraints (12):
    c: Coincident(g0,g1)
    c: Coincident(g1,g2)
    c: Coincident(g2,g3)
    c: Coincident(g3,g0)
    c: Horizontal(g0)
    c: Horizontal(g2)
    c: Vertical(g1)
    c: Vertical(g3)
    c: DistanceX(g2,g2) = 3
    c: DistanceY(g1,g1) = 5.8
    c: DistanceY(g-1,g0) = 7.1
    c: DistanceX(g-1,g0) = 21.5
FEATURE [Sketcher::SketchObject] Sketch1456
  MapMode = 5
  Placement = pos=(0,10,-2.2e-15) rot=(1,0,0;1.5708rad)
  Support = -> [Fillet168]
  sketch-geometry (4):
    g0: LineSegment StartX=76.5 StartY=25 StartZ=0 EndX=117 EndY=25 EndZ=0
    g1: LineSegment StartX=117 StartY=25 StartZ=0 EndX=117 EndY=5 EndZ=0
    g2: LineSegment StartX=117 StartY=5 StartZ=0 EndX=76.5 EndY=5 EndZ=0
    g3: LineSegment StartX=76.5 StartY=5 StartZ=0 EndX=76.5 EndY=25 EndZ=0
  constraints (12):
    c: Coincident(g0,g1)
    c: Coincident(g1,g2)
    c: Coincident(g2,g3)
    c: Coincident(g3,g0)
    c: Horizontal(g0)
    c: Horizontal(g2)
    c: Vertical(g1)
    c: Vertical(g3)
    c: DistanceX(g0,g0) = 40.5
    c: DistanceY(g3,g3) = 20
    c: DistanceY(g-1,g2) = 5
    c: DistanceX(g-1,g2) = 76.5
FEATURE [PartDesign::Pocket] Pocket458  label="Servo Pocket009"
  BaseFeature = -> Fillet168
  Length = 30
  Length2 = 100
  Profile = -> Sketch1456
  Type = 0
FEATURE [PartDesign::Fillet] Fillet169  label="Smooth Mount Edges005"
  Base = -> Pocket458 [Edge147,Edge146,Edge141,Edge152]
  BaseFeature = -> Pocket458
  Radius = 0.4
FEATURE [Sketcher::SketchObject] Sketch1335
  MapMode = 5
  Placement = pos=(0,0,0) rot=(1,0,0;3.14159rad)
  Support = -> [Fillet169]
  sketch-geometry (11):
    g0: LineSegment StartX=0 StartY=-43.25 StartZ=0 EndX=120.25 EndY=-43.25 EndZ=0
    g1: ArcOfCircle CenterX=120.25 CenterY=-38.25 CenterZ=0 NormalX=0 NormalY=0 NormalZ=1 AngleXU=0 Radius=5 StartAngle=4.71239 EndAngle=6.28319
    g2: LineSegment StartX=125.25 StartY=-38.25 StartZ=0 EndX=125.25 EndY=-14.75 EndZ=0
    g3: LineSegment StartX=125.25 StartY=-14.75 StartZ=0 EndX=117 EndY=-14.75 EndZ=0
    g4: LineSegment StartX=117 StartY=-14.75 StartZ=0 EndX=117 EndY=0 EndZ=0
    g5: LineSegment StartX=117 StartY=0 StartZ=0 EndX=0 EndY=0 EndZ=0
    g6: LineSegment StartX=0 StartY=0 StartZ=0 EndX=0 EndY=-14.25 EndZ=0
    g7: LineSegment StartX=0 StartY=-14.25 StartZ=0 EndX=39.75 EndY=-14.25 EndZ=0
    g8: LineSegment StartX=39.75 StartY=-14.25 StartZ=0 EndX=39.75 EndY=-25.75 EndZ=0
    g9: LineSegment StartX=39.75 StartY=-25.75 StartZ=0 EndX=0 EndY=-25.75 EndZ=0
    g10: LineSegment StartX=0 StartY=-25.75 StartZ=0 EndX=0 EndY=-43.25 EndZ=0
  constraints (30):
    c: PointOnObject(g0,g-2)
    c: Horizontal(g0)
    c: Tangent(g0,g1) = -1.5708
    c: Tangent(g1,g2) = -1.5708
    c: Coincident(g2,g3)
    c: Coincident(g3,g4)
    c: Coincident(g4,g5)
    c: Coincident(g5,g-1)
    c: Coincident(g5,g6)
    c: Coincident(g10,g0)
    c: Horizontal(g3)
    c: Vertical(g4)
    c: Vertical(g2)
    c: Horizontal(g5)
    c: DistanceX(g5,g2) = 125.25
    c: Radius(g1) = 5
    c: DistanceY(g4,g4) = 14.75
    c: DistanceX(g3,g3) = 8.25
    c: DistanceY(g0,g4) = 43.25
    c: Horizontal(g7)
    c: Coincident(g7,g8)
    c: Vertical(g8)
    c: Coincident(g8,g9)
    c: Horizontal(g9)
    c: Coincident(g6,g7)
    c: Tangent(g6,g10)
    c: DistanceY(g8,g8) = 11.5
    c: DistanceX(g7,g7) = 39.75
    c: DistanceY(g6,g5) = 14.25
    c: Coincident(g9,g10)
FEATURE [PartDesign::Pocket] Pocket517  label="Bottom Removal and Interlock002"
  BaseFeature = -> Fillet169
  Length = 25
  Length2 = 100
  Profile = -> Sketch1335
  Type = 0
FEATURE [Sketcher::SketchObject] Sketch1441
  MapMode = 5
  Placement = pos=(0,0,0) rot=(1,0,0;3.14159rad)
  Support = -> [Pocket517]
  sketch-geometry (4):
    g0: LineSegment StartX=0 StartY=-26 StartZ=0 EndX=40 EndY=-26 EndZ=0
    g1: LineSegment StartX=40 StartY=-26 StartZ=0 EndX=40 EndY=-14 EndZ=0
    g2: LineSegment StartX=40 StartY=-14 StartZ=0 EndX=0 EndY=-14 EndZ=0
    g3: LineSegment StartX=0 StartY=-14 StartZ=0 EndX=0 EndY=-26 EndZ=0
  constraints (12):
    c: Coincident(g0,g1)
    c: Coincident(g1,g2)
    c: Coincident(g2,g3)
    c: Coincident(g3,g0)
    c: Horizontal(g0)
    c: Horizontal(g2)
    c: Vertical(g1)
    c: Vertical(g3)
    c: PointOnObject(g0,g-2)
    c: DistanceY(g1,g1) = 12
    c: DistanceY(g2,g-1) = 14
    c: DistanceX(g0,g0) = 40
FEATURE [PartDesign::Pocket] Pocket450  label="Shorten Interlock002"
  BaseFeature = -> Pocket517
  Length = 5
  Length2 = 100
  Profile = -> Sketch1441
  Type = 0
FEATURE [Sketcher::SketchObject] Sketch1457
  MapMode = 5
  Support = -> [XY_Plane503]
  sketch-geometry (8):
    g0: LineSegment StartX=0 StartY=3.17543 StartZ=0 EndX=-2.75 EndY=1.58771 EndZ=0
    g1: LineSegment StartX=-2.75 StartY=1.58771 StartZ=0 EndX=-2.75 EndY=-1.58771 EndZ=0
    g2: LineSegment StartX=-2.75 StartY=-1.58771 StartZ=0 EndX=0 EndY=-3.17543 EndZ=0
    g3: LineSegment StartX=0 StartY=-3.17543 StartZ=0 EndX=2.75 EndY=-1.58771 EndZ=0
    g4: LineSegment StartX=2.75 StartY=-1.58771 StartZ=0 EndX=2.75 EndY=1.58771 EndZ=0
    g5: LineSegment StartX=2.75 StartY=1.58771 StartZ=0 EndX=0 EndY=3.17543 EndZ=0
    g6: Circle [constr] CenterX=0 CenterY=0 CenterZ=0 NormalX=0 NormalY=0 NormalZ=1 AngleXU=0 Radius=3.17543
    g7: Circle CenterX=0 CenterY=0 CenterZ=0 NormalX=0 NormalY=0 NormalZ=1 AngleXU=0 Radius=1.5
  constraints (18):
    c: Coincident(g0,g1)
    c: Coincident(g1,g2)
    c: Coincident(g2,g3)
    c: Coincident(g3,g4)
    c: Coincident(g4,g5)
    c: Coincident(g5,g0)
    c: Equal(g0, g1-g5) x5
    c: PointOnObject(g0,g6)
    c: PointOnObject(g1,g6)
    c: PointOnObject(g2,g6)
    c: PointOnObject(g3,g6)
    c: PointOnObject(g4,g6)
    c: PointOnObject(g5,g6)
    c: Coincident(g6,g-1)
    c: PointOnObject(g5,g-2)
    c: DistanceX(g0,g4) = 5.5
    c: Coincident(g7,g-1)
    c: Radius(g7) = 1.5
FEATURE [PartDesign::Pad] Pad497  label="M3 Nut Primitive095"
  Length = 1.2
  Length2 = 1.2
  Profile = -> Sketch1457
  Type = 4
FEATURE [Sketcher::SketchObject] Sketch1449
  ExternalGeometry = -> [Pad497]
  MapMode = 5
  Placement = pos=(0,0,0) rot=(0.57735,0.57735,0.57735;2.0944rad)
  Support = -> [YZ_Plane505]
  sketch-geometry (6):
    g0: LineSegment StartX=-2.67543 StartY=1.2 StartZ=0 EndX=-3.67543 EndY=1.2 EndZ=0
    g1: LineSegment StartX=-3.67543 StartY=1.2 StartZ=0 EndX=-3.67543 EndY=-1.2 EndZ=0
    g2: LineSegment StartX=-3.67543 StartY=-1.2 StartZ=0 EndX=-2.67543 EndY=-1.2 EndZ=0
    g3: LineSegment StartX=-2.67543 StartY=-1.2 StartZ=0 EndX=-3.17543 EndY=-1 EndZ=0
    g4: LineSegment StartX=-3.17543 StartY=-1 StartZ=0 EndX=-3.17543 EndY=1 EndZ=0
    g5: LineSegment StartX=-3.17543 StartY=1 StartZ=0 EndX=-2.67543 EndY=1.2 EndZ=0
  constraints (15):
    c: Horizontal(g0)
    c: Coincident(g0,g1)
    c: Coincident(g1,g2)
    c: Coincident(g2,g3)
    c: Coincident(g3,g4)
    c: Coincident(g4,g5)
    c: Coincident(g5,g0)
    c: Symmetric(g4,g3,g-1)
    c: Symmetric(g0,g2,g-1)
    c: Symmetric(g1,g0,g-1)
    c: DistanceX(g0,g4) = 0.5
    c: DistanceY(g3,g4) = 2
    c: DistanceY(g1,g0) = 2.4
    c: PointOnObject(g3,g-3)
    c: DistanceX(g4,g0) = 0.5
FEATURE [PartDesign::Groove] Groove115  label="M3 Nut Smooth109"
  Angle = 360
  Axis = (-2e-16,3e-16,1)
  Base = (0,0,0)
  BaseFeature = -> Pad497
  Profile = -> Sketch1449
  ReferenceAxis = -> Sketch1449 [V_Axis]
  Reversed = true
FEATURE [PartDesign::Chamfer] Chamfer260  label="M3 Nut Smooth Hole111"
  Base = -> Groove115 [Edge24,Edge23]
  BaseFeature = -> Groove115
  Size = 0.2
FEATURE [PartDesign::Body] Body320  label="M3 Nut054"
  Group = -> [Sketch1457,Pad497,Sketch1449,Groove115,Chamfer260]
  Origin = -> Origin533
  Placement = pos=(-110.55,7.7,52.05) rot=(0.57735,0.57735,-0.57735;2.0944rad)
  Tip = -> Chamfer260
FEATURE [Sketcher::SketchObject] Sketch1458
  MapMode = 5
  Placement = pos=(0,52,0) rot=(0,0.707107,0.707107;3.14159rad)
  Support = -> [Pocket450]
  sketch-geometry (3):
    g0: Circle [constr] CenterX=0 CenterY=0 CenterZ=0 NormalX=0 NormalY=0 NormalZ=1 AngleXU=0 Radius=35
    g1: Circle CenterX=-28.7228 CenterY=20 CenterZ=0 NormalX=0 NormalY=0 NormalZ=1 AngleXU=0 Radius=1.6
    g2: Circle CenterX=-33.541 CenterY=10 CenterZ=0 NormalX=0 NormalY=0 NormalZ=1 AngleXU=0 Radius=1.6
  constraints (8):
    c: Coincident(g0,g-1)
    c: Radius(g0) = 35
    c: PointOnObject(g1,g0)
    c: PointOnObject(g2,g0)
    c: Equal(g2,g1)
    c: Radius(g1) = 1.6
    c: DistanceY(g2,g1) = 10
    c: DistanceY(g-1,g2) = 10
FEATURE [PartDesign::Pocket] Pocket441  label="Screwholes Ball Bearing Mount (Interlock)002"
  BaseFeature = -> Pocket450
  Length = 22
  Length2 = 100
  Profile = -> Sketch1458
  Type = 0
FEATURE [Sketcher::SketchObject] Sketch1440
  MapMode = 5
  Placement = pos=(0,14.25,0) rot=(1,0,0;1.5708rad)
  Support = -> [Pocket441]
  sketch-geometry (3):
    g0: Circle [constr] CenterX=0 CenterY=0 CenterZ=0 NormalX=0 NormalY=0 NormalZ=1 AngleXU=0 Radius=35
    g1: Circle CenterX=28.7228 CenterY=20 CenterZ=0 NormalX=0 NormalY=0 NormalZ=1 AngleXU=0 Radius=1.6
    g2: Circle CenterX=33.541 CenterY=10 CenterZ=0 NormalX=0 NormalY=0 NormalZ=1 AngleXU=0 Radius=1.6
  constraints (8):
    c: Coincident(g0,g-1)
    c: PointOnObject(g1,g0)
    c: PointOnObject(g2,g0)
    c: Equal(g2,g1)
    c: Radius(g1) = 1.6
    c: DistanceY(g2,g1) = 10
    c: DistanceY(g-1,g2) = 10
    c: Radius(g0) = 35
FEATURE [PartDesign::Pocket] Pocket443  label="Screwholes Servohorn Mount005"
  BaseFeature = -> Pocket441
  Length = 10
  Length2 = 100
  Profile = -> Sketch1440
  Type = 0
FEATURE [PartDesign::Pocket] Pocket456  label="Bottom Nuthole Ball Bearing Mount (Interlock)002"
  BaseFeature = -> Pocket443
  Length = 38
  Length2 = 100
  Profile = -> Sketch1454
  Reversed = true
  Type = 0
FEATURE [PartDesign::Pocket] Pocket514  label="Top Nuthole Ball Bearing Mount (Interlock)002"
  BaseFeature = -> Pocket456
  Length = 33
  Length2 = 100
  Profile = -> Sketch1452
  Reversed = true
  Type = 0
FEATURE [Sketcher::SketchObject] Sketch1459
  MapMode = 5
  Support = -> [XY_Plane498]
  sketch-geometry (2):
    g0: Circle CenterX=0 CenterY=0 CenterZ=0 NormalX=0 NormalY=0 NormalZ=1 AngleXU=0 Radius=4
    g1: Circle CenterX=0 CenterY=0 CenterZ=0 NormalX=0 NormalY=0 NormalZ=1 AngleXU=0 Radius=6.25
  constraints (4):
    c: Coincident(g0,g-1)
    c: Coincident(g1,g0)
    c: Radius(g0) = 4
    c: Radius(g1) = 6.25
FEATURE [PartDesign::Pad] Pad480
  Length = 5
  Length2 = 100
  Profile = -> Sketch1459
  Type = 0
FEATURE [PartDesign::Chamfer] Chamfer235
  Base = -> Pad480 [Face3,Face4]
  BaseFeature = -> Pad480
  Size = 0.2
FEATURE [PartDesign::Body] Body335
  Group = -> [Sketch1459,Pad480,Chamfer235]
  Origin = -> Origin501
  Tip = -> Chamfer235
FEATURE [Sketcher::SketchObject] Sketch1461
  MapMode = 5
  Placement = pos=(0,10,-2.2e-15) rot=(1,0,0;1.5708rad)
  Support = -> [Pocket514]
  sketch-geometry (2):
    g0: Circle CenterX=121 CenterY=20 CenterZ=0 NormalX=0 NormalY=0 NormalZ=1 AngleXU=0 Radius=1.6
    g1: Circle CenterX=121 CenterY=10 CenterZ=0 NormalX=0 NormalY=0 NormalZ=1 AngleXU=0 Radius=1.6
  constraints (6):
    c: Vertical(g1,g0)
    c: Equal(g0,g1)
    c: Radius(g0) = 1.6
    c: DistanceY(g1,g0) = 10
    c: DistanceX(g-1,g1) = 121
    c: DistanceY(g-1,g1) = 10
FEATURE [PartDesign::Pocket] Pocket454  label="Screwholes Servopocket004"
  BaseFeature = -> Pocket514
  Length = 6
  Length2 = 100
  Profile = -> Sketch1461
  Type = 0
FEATURE [Sketcher::SketchObject] Sketch1451
  MapMode = 5
  Placement = pos=(0,0,25) rot=(1,0,0;3.14159rad)
  Support = -> [Pocket454]
  sketch-geometry (4):
    g0: LineSegment StartX=125 StartY=-26 StartZ=0 EndX=125 EndY=-34.5 EndZ=0
    g1: LineSegment StartX=125 StartY=-34.5 StartZ=0 EndX=30 EndY=-34.5 EndZ=0
    g2: LineSegment StartX=30 StartY=-26 StartZ=0 EndX=125 EndY=-26 EndZ=0
    g3: LineSegment StartX=30 StartY=-34.5 StartZ=0 EndX=30 EndY=-26 EndZ=0
  constraints (12):
    c: Coincident(g0,g1)
    c: Horizontal(g1)
    c: Vertical(g0)
    c: DistanceX(g-1,g0) = 125
    c: Coincident(g3,g2)
    c: Horizontal(g2)
    c: Vertical(g3)
    c: DistanceY(g3,g3) = 8.5
    c: DistanceY(g2,g-1) = 26
    c: DistanceX(g-1,g2) = 30
    c: Coincident(g3,g1)
    c: Coincident(g0,g2)
FEATURE [PartDesign::Pocket] Pocket451  label="Cableguide002"
  BaseFeature = -> Pocket454
  Length = 2
  Length2 = 100
  Profile = -> Sketch1451
  Type = 0
FEATURE [PartDesign::Fillet] Fillet172  label="Smooth Corners Cableguide002"
  Base = -> Pocket451 [Edge183,Edge184,Edge188,Edge186]
  BaseFeature = -> Pocket451
  Radius = 1
FEATURE [PartDesign::Fillet] Fillet175  label="Smooth Interlock005"
  Base = -> Fillet172 [Edge89,Edge85,Edge79,Edge86,Edge78,Edge148,Edge80,Edge87,Edge27,Edge23,Edge25,Edge84]
  BaseFeature = -> Fillet172
  Radius = 0.2
FEATURE [Sketcher::SketchObject] Sketch1462
  MapMode = 5
  Support = -> [XY_Plane564]
  sketch-geometry (8):
    g0: LineSegment StartX=0 StartY=3.17543 StartZ=0 EndX=-2.75 EndY=1.58771 EndZ=0
    g1: LineSegment StartX=-2.75 StartY=1.58771 StartZ=0 EndX=-2.75 EndY=-1.58771 EndZ=0
    g2: LineSegment StartX=-2.75 StartY=-1.58771 StartZ=0 EndX=0 EndY=-3.17543 EndZ=0
    g3: LineSegment StartX=0 StartY=-3.17543 StartZ=0 EndX=2.75 EndY=-1.58771 EndZ=0
    g4: LineSegment StartX=2.75 StartY=-1.58771 StartZ=0 EndX=2.75 EndY=1.58771 EndZ=0
    g5: LineSegment StartX=2.75 StartY=1.58771 StartZ=0 EndX=0 EndY=3.17543 EndZ=0
    g6: Circle [constr] CenterX=0 CenterY=0 CenterZ=0 NormalX=0 NormalY=0 NormalZ=1 AngleXU=0 Radius=3.17543
    g7: Circle CenterX=0 CenterY=0 CenterZ=0 NormalX=0 NormalY=0 NormalZ=1 AngleXU=0 Radius=1.5
  constraints (18):
    c: Coincident(g0,g1)
    c: Coincident(g1,g2)
    c: Coincident(g2,g3)
    c: Coincident(g3,g4)
    c: Coincident(g4,g5)
    c: Coincident(g5,g0)
    c: Equal(g0, g1-g5) x5
    c: PointOnObject(g0,g6)
    c: PointOnObject(g1,g6)
    c: PointOnObject(g2,g6)
    c: PointOnObject(g3,g6)
    c: PointOnObject(g4,g6)
    c: PointOnObject(g5,g6)
    c: Coincident(g6,g-1)
    c: PointOnObject(g5,g-2)
    c: DistanceX(g0,g4) = 5.5
    c: Coincident(g7,g-1)
    c: Radius(g7) = 1.5
FEATURE [PartDesign::Pad] Pad492  label="M3 Nut Primitive093"
  Length = 1.2
  Length2 = 1.2
  Profile = -> Sketch1462
  Type = 4
FEATURE [Sketcher::SketchObject] Sketch1463
  MapMode = 5
  Placement = pos=(0,0,26.6) rot=(0,0,1;0rad)
  Support = -> [Pad493]
  sketch-geometry (4):
    g0: LineSegment StartX=-10 StartY=-26.8 StartZ=0 EndX=10 EndY=-26.8 EndZ=0
    g1: LineSegment StartX=10 StartY=-26.8 StartZ=0 EndX=10 EndY=26.8 EndZ=0
    g2: LineSegment StartX=10 StartY=26.8 StartZ=0 EndX=-10 EndY=26.8 EndZ=0
    g3: LineSegment StartX=-10 StartY=26.8 StartZ=0 EndX=-10 EndY=-26.8 EndZ=0
  constraints (10):
    c: Coincident(g0,g1)
    c: Coincident(g1,g2)
    c: Coincident(g2,g3)
    c: Coincident(g3,g0)
    c: Horizontal(g0)
    c: Vertical(g3)
    c: Symmetric(g1,g2,g-2)
    c: Symmetric(g1,g0,g-1)
    c: DistanceX(g2,g2) = 20
    c: DistanceY(g1,g1) = 53.6
FEATURE [PartDesign::Pad] Pad580
  BaseFeature = -> Pad493
  Length = 2.5
  Length2 = 100
  Profile = -> Sketch1463
  Type = 0
FEATURE [Sketcher::SketchObject] Sketch1371
  MapMode = 5
  Placement = pos=(0,0,29.1) rot=(0,0,1;0rad)
  Support = -> [Pad580]
  sketch-geometry (4):
    g0: LineSegment StartX=-10 StartY=-20.15 StartZ=0 EndX=10 EndY=-20.15 EndZ=0
    g1: LineSegment StartX=10 StartY=-20.15 StartZ=0 EndX=10 EndY=20.15 EndZ=0
    g2: LineSegment StartX=10 StartY=20.15 StartZ=0 EndX=-10 EndY=20.15 EndZ=0
    g3: LineSegment StartX=-10 StartY=20.15 StartZ=0 EndX=-10 EndY=-20.15 EndZ=0
  constraints (10):
    c: Coincident(g0,g1)
    c: Coincident(g1,g2)
    c: Coincident(g2,g3)
    c: Coincident(g3,g0)
    c: Horizontal(g0)
    c: Vertical(g3)
    c: Symmetric(g1,g2,g-2)
    c: Symmetric(g1,g0,g-1)
    c: DistanceX(g2,g2) = 20
    c: DistanceY(g1,g1) = 40.3
FEATURE [PartDesign::Pad] Pad489
  BaseFeature = -> Pad580
  Length = 6
  Length2 = 100
  Profile = -> Sketch1371
  Type = 0
FEATURE [Sketcher::SketchObject] Sketch1399
  ExternalGeometry = -> [Pad489]
  MapMode = 5
  Placement = pos=(0,0,35.1) rot=(0,0,1;0rad)
  Support = -> [Pad489]
  sketch-geometry (7):
    g0: ArcOfCircle CenterX=-3e-16 CenterY=10.15 CenterZ=0 NormalX=0 NormalY=0 NormalZ=1 AngleXU=0 Radius=9.5 StartAngle=5.9573 EndAngle=9.75066
    g1: LineSegment StartX=-9 StartY=7.10862 StartZ=0 EndX=-9 EndY=-14.15 EndZ=0
    g2: LineSegment StartX=-9 StartY=-14.15 StartZ=0 EndX=-5 EndY=-14.15 EndZ=0
    g3: LineSegment StartX=5 StartY=-14.15 StartZ=0 EndX=9 EndY=-14.15 EndZ=0
    g4: LineSegment StartX=9 StartY=-14.15 StartZ=0 EndX=9 EndY=7.10862 EndZ=0
    g5: ArcOfCircle CenterX=-3e-16 CenterY=-10.4 CenterZ=0 NormalX=0 NormalY=0 NormalZ=1 AngleXU=0 Radius=6.25 StartAngle=3.78509 EndAngle=5.63968
    g6: LineSegment [constr] StartX=0 StartY=-20.15 StartZ=0 EndX=0 EndY=-16.65 EndZ=0
  constraints (22):
    c: Symmetric(g0,g0,g-2)
    c: Coincident(g1,g0)
    c: Vertical(g1)
    c: Coincident(g2,g1)
    c: Horizontal(g2)
    c: Horizontal(g3)
    c: Coincident(g4,g3)
    c: Coincident(g4,g0)
    c: Vertical(g4)
    c: Symmetric(g2,g3,g-2)
    c: Coincident(g5,g2)
    c: Coincident(g5,g3)
    c: DistanceY(g-3,g3) = 6
    c: DistanceY(g0,g-4) = 10
    c: Radius(g0) = 9.5
    c: DistanceX(g0,g0) = 18
    c: PointOnObject(g6,g-3)
    c: PointOnObject(g6,g5)
    c: Vertical(g6)
    c: DistanceY(g6,g6) = 3.5
    c: DistanceX(g2,g3) = 10
    c: PointOnObject(g6,g-2)
FEATURE [PartDesign::Pad] Pad581
  BaseFeature = -> Pad489
  Length = 2.5
  Length2 = 100
  Profile = -> Sketch1399
  Type = 0
FEATURE [Sketcher::SketchObject] Sketch1381
  ExternalGeometry = -> [Pad581]
  MapMode = 5
  Placement = pos=(0,0,37.6) rot=(0,0,1;0rad)
  Support = -> [Pad581]
  sketch-geometry (1):
    g0: Circle CenterX=-3e-16 CenterY=10.15 CenterZ=0 NormalX=0 NormalY=0 NormalZ=1 AngleXU=0 Radius=6.5
  constraints (2):
    c: Coincident(g0,g-3)
    c: Radius(g0) = 6.5
FEATURE [PartDesign::Pad] Pad590
  BaseFeature = -> Pad581
  Length = 1
  Length2 = 100
  Profile = -> Sketch1381
  Type = 0
FEATURE [Sketcher::SketchObject] Sketch1374
  ExternalGeometry = -> [Pad590]
  MapMode = 5
  Placement = pos=(0,0,38.6) rot=(0,0,1;0rad)
  Support = -> [Pad590]
  sketch-geometry (1):
    g0: Circle CenterX=0 CenterY=10.15 CenterZ=0 NormalX=0 NormalY=0 NormalZ=1 AngleXU=0 Radius=5.5
  constraints (2):
    c: Coincident(g0,g-3)
    c: Radius(g0) = 5.5
FEATURE [PartDesign::Pad] Pad582
  BaseFeature = -> Pad590
  Length = 0.5
  Length2 = 100
  Profile = -> Sketch1374
  Type = 0
FEATURE [Sketcher::SketchObject] Sketch1396
  ExternalGeometry = -> [Pad582]
  MapMode = 5
  Placement = pos=(0,0,39.1) rot=(0,0,1;0rad)
  Support = -> [Pad582]
  sketch-geometry (1):
    g0: Circle CenterX=0 CenterY=10.15 CenterZ=0 NormalX=0 NormalY=0 NormalZ=1 AngleXU=0 Radius=3
  constraints (2):
    c: Coincident(g0,g-3)
    c: Radius(g0) = 3
FEATURE [PartDesign::Pad] Pad500
  BaseFeature = -> Pad582
  Length = 4
  Length2 = 100
  Profile = -> Sketch1396
  Type = 0
FEATURE [Sketcher::SketchObject] Sketch1405
  ExternalGeometry = -> [Pad500]
  MapMode = 5
  Placement = pos=(0,0,43.1) rot=(0,0,1;0rad)
  Support = -> [Pad500]
  sketch-geometry (1):
    g0: Circle CenterX=0 CenterY=10.15 CenterZ=0 NormalX=0 NormalY=0 NormalZ=1 AngleXU=0 Radius=1.5
  constraints (2):
    c: Coincident(g0,g-3)
    c: Radius(g0) = 1.5
FEATURE [PartDesign::Pocket] Pocket519
  BaseFeature = -> Pad500
  Length = 5
  Length2 = 100
  Profile = -> Sketch1405
  Type = 0
FEATURE [Sketcher::SketchObject] Sketch1391
  MapMode = 5
  Placement = pos=(0,0,29.1) rot=(0,0,1;0rad)
  Support = -> [Pocket519]
  sketch-geometry (4):
    g0: Circle CenterX=-4.91157 CenterY=25.3 CenterZ=0 NormalX=0 NormalY=0 NormalZ=1 AngleXU=0 Radius=2.25
    g1: Circle CenterX=4.91157 CenterY=25.3 CenterZ=0 NormalX=0 NormalY=0 NormalZ=1 AngleXU=0 Radius=2.25
    g2: Circle CenterX=-4.91157 CenterY=-25.3 CenterZ=0 NormalX=0 NormalY=0 NormalZ=1 AngleXU=0 Radius=2.25
    g3: Circle CenterX=4.91157 CenterY=-25.3 CenterZ=0 NormalX=0 NormalY=0 NormalZ=1 AngleXU=0 Radius=2.25
  constraints (8):
    c: Equal(g3,g2)
    c: Equal(g2,g1)
    c: Equal(g1,g0)
    c: Radius(g1) = 2.25
    c: Symmetric(g1,g0,g-2)
    c: Symmetric(g3,g2,g-2)
    c: Symmetric(g3,g1,g-1)
    c: DistanceY(g3,g1) = 50.6
FEATURE [PartDesign::Pocket] Pocket512
  BaseFeature = -> Pocket519
  Length = 5
  Length2 = 100
  Profile = -> Sketch1391
  Type = 0
FEATURE [Sketcher::SketchObject] Sketch1377
  MapMode = 5
  Placement = pos=(0,0,29.1) rot=(0,0,1;0rad)
  Support = -> [Pocket512]
  sketch-geometry (8):
    g0: LineSegment StartX=-0.5 StartY=26.8 StartZ=0 EndX=0.5 EndY=26.8 EndZ=0
    g1: LineSegment StartX=0.5 StartY=26.8 StartZ=0 EndX=0.5 EndY=20.15 EndZ=0
    g2: LineSegment StartX=0.5 StartY=20.15 StartZ=0 EndX=-0.5 EndY=20.15 EndZ=0
    g3: LineSegment StartX=-0.5 StartY=20.15 StartZ=0 EndX=-0.5 EndY=26.8 EndZ=0
    g4: LineSegment StartX=-0.5 StartY=-20.15 StartZ=0 EndX=0.5 EndY=-20.15 EndZ=0
    g5: LineSegment StartX=0.5 StartY=-20.15 StartZ=0 EndX=0.5 EndY=-26.8 EndZ=0
    g6: LineSegment StartX=0.5 StartY=-26.8 StartZ=0 EndX=-0.5 EndY=-26.8 EndZ=0
    g7: LineSegment StartX=-0.5 StartY=-26.8 StartZ=0 EndX=-0.5 EndY=-20.15 EndZ=0
  constraints (20):
    c: Coincident(g0,g1)
    c: Coincident(g1,g2)
    c: Coincident(g2,g3)
    c: Coincident(g3,g0)
    c: Horizontal(g2)
    c: Vertical(g1)
    c: Vertical(g3)
    c: Coincident(g4,g5)
    c: Coincident(g5,g6)
    c: Coincident(g6,g7)
    c: Coincident(g7,g4)
    c: Horizontal(g6)
    c: Vertical(g7)
    c: Symmetric(g4,g4,g-2)
    c: Symmetric(g0,g0,g-2)
    c: Symmetric(g0,g5,g-1)
    c: DistanceY(g5,g0) = 53.6
    c: DistanceY(g4,g1) = 40.3
    c: DistanceX(g0,g0) = 1
    c: Symmetric(g4,g1,g-1)
FEATURE [PartDesign::Pad] Pad574
  BaseFeature = -> Pocket512
  Length = 2
  Length2 = 100
  Profile = -> Sketch1377
  Type = 0
FEATURE [Sketcher::SketchObject] Sketch1404
  ExternalGeometry = -> [Pad574]
  MapMode = 5
  Placement = pos=(0.5,0,0) rot=(0.57735,0.57735,0.57735;2.0944rad)
  Support = -> [Pad574]
  sketch-geometry (6):
    g0: LineSegment StartX=-26.8 StartY=29.1 StartZ=0 EndX=-26.8 EndY=31.1 EndZ=0
    g1: LineSegment StartX=-26.8 StartY=31.1 StartZ=0 EndX=-20.15 EndY=31.1 EndZ=0
    g2: LineSegment StartX=-20.15 StartY=31.1 StartZ=0 EndX=-26.8 EndY=29.1 EndZ=0
    g3: LineSegment StartX=20.15 StartY=31.1 StartZ=0 EndX=26.8 EndY=31.1 EndZ=0
    g4: LineSegment StartX=26.8 StartY=31.1 StartZ=0 EndX=26.8 EndY=29.1 EndZ=0
    g5: LineSegment StartX=26.8 StartY=29.1 StartZ=0 EndX=20.15 EndY=31.1 EndZ=0
  constraints (14):
    c: Vertical(g0)
    c: Coincident(g0,g1)
    c: Horizontal(g1)
    c: Coincident(g1,g2)
    c: Coincident(g2,g0)
    c: Coincident(g3,g4)
    c: Coincident(g4,g5)
    c: Coincident(g5,g3)
    c: Symmetric(g0,g4,g-2)
    c: Symmetric(g3,g0,g-2)
    c: Symmetric(g1,g3,g-2)
    c: DistanceX(g0,g3) = 53.6
    c: DistanceY(g4,g4) = 2
    c: Coincident(g3,g-3)
FEATURE [PartDesign::Pocket] Pocket529
  BaseFeature = -> Pad574
  Length = 1
  Length2 = 100
  Profile = -> Sketch1404
  Type = 0
FEATURE [PartDesign::Fillet] Fillet160
  Base = -> Pocket529 [Edge26,Edge27,Edge72,Edge63,Edge70,Edge78,Edge51,Edge49,Edge71,Edge50,Edge79,Edge86,Edge30,Edge21,Edge4,Edge29,Edge105,Edge107,Edge109,Edge111,Edge113,Edge114,Edge123]
  BaseFeature = -> Pocket529
  Radius = 0.4
FEATURE [Sketcher::SketchObject] Sketch1407
  MapMode = 5
  Placement = pos=(0,20.15,0) rot=(0,0.707107,0.707107;3.14159rad)
  Support = -> [Fillet160]
  sketch-geometry (4):
    g0: LineSegment StartX=-3.25 StartY=2 StartZ=0 EndX=3.25 EndY=2 EndZ=0
    g1: LineSegment StartX=3.25 StartY=2 StartZ=0 EndX=3.25 EndY=6 EndZ=0
    g2: LineSegment StartX=3.25 StartY=6 StartZ=0 EndX=-3.25 EndY=6 EndZ=0
    g3: LineSegment StartX=-3.25 StartY=6 StartZ=0 EndX=-3.25 EndY=2 EndZ=0
  constraints (11):
    c: Coincident(g0,g1)
    c: Coincident(g1,g2)
    c: Coincident(g2,g3)
    c: Coincident(g3,g0)
    c: Horizontal(g0)
    c: Vertical(g1)
    c: Vertical(g3)
    c: DistanceY(g-1,g0) = 2
    c: DistanceY(g1,g1) = 4
    c: Symmetric(g2,g1,g-2)
    c: DistanceX(g2,g2) = 6.5
FEATURE [PartDesign::Pad] Pad496
  BaseFeature = -> Fillet160
  Length = 1
  Length2 = 100
  Profile = -> Sketch1407
  Type = 0
FEATURE [Sketcher::SketchObject] Sketch1373
  MapMode = 5
  Placement = pos=(0,21.15,0) rot=(0,0.707107,0.707107;3.14159rad)
  Support = -> [Pad496]
  sketch-geometry (4):
    g0: LineSegment StartX=-2.75 StartY=5.5 StartZ=0 EndX=2.75 EndY=5.5 EndZ=0
    g1: LineSegment StartX=2.75 StartY=5.5 StartZ=0 EndX=2.75 EndY=2.5 EndZ=0
    g2: LineSegment StartX=2.75 StartY=2.5 StartZ=0 EndX=-2.75 EndY=2.5 EndZ=0
    g3: LineSegment StartX=-2.75 StartY=2.5 StartZ=0 EndX=-2.75 EndY=5.5 EndZ=0
  constraints (11):
    c: Coincident(g0,g1)
    c: Coincident(g1,g2)
    c: Coincident(g2,g3)
    c: Coincident(g3,g0)
    c: Horizontal(g0)
    c: Vertical(g1)
    c: Vertical(g3)
    c: Symmetric(g1,g2,g-2)
    c: DistanceY(g1,g0) = 3
    c: DistanceY(g-1,g1) = 2.5
    c: DistanceX(g0,g0) = 5.5
FEATURE [PartDesign::Pad] Pad589
  BaseFeature = -> Pad496
  Length = 4
  Length2 = 100
  Profile = -> Sketch1373
  Type = 0
FEATURE [Sketcher::SketchObject] Sketch1383
  MapMode = 5
  Placement = pos=(0,0,0) rot=(1,0,0;3.14159rad)
  Support = -> [Pad589]
  sketch-geometry (4):
    g0: LineSegment StartX=-10 StartY=-20.15 StartZ=0 EndX=10 EndY=-20.15 EndZ=0
    g1: LineSegment StartX=10 StartY=-20.15 StartZ=0 EndX=10 EndY=20.15 EndZ=0
    g2: LineSegment StartX=10 StartY=20.15 StartZ=0 EndX=-10 EndY=20.15 EndZ=0
    g3: LineSegment StartX=-10 StartY=20.15 StartZ=0 EndX=-10 EndY=-20.15 EndZ=0
  constraints (10):
    c: Coincident(g0,g1)
    c: Coincident(g1,g2)
    c: Coincident(g2,g3)
    c: Coincident(g3,g0)
    c: Horizontal(g0)
    c: Vertical(g1)
    c: Symmetric(g2,g1,g-2)
    c: Symmetric(g0,g2,g-1)
    c: DistanceX(g2,g2) = 20
    c: DistanceY(g1,g1) = 40.3
FEATURE [PartDesign::Pad] Pad577
  BaseFeature = -> Pad589
  Length = 2
  Length2 = 100
  Profile = -> Sketch1383
  Type = 0
FEATURE [PartDesign::Chamfer] Chamfer218
  Base = -> Pad577 [Face7]
  BaseFeature = -> Pad577
  Size = 1.5
FEATURE [PartDesign::Fillet] Fillet165
  Base = -> Chamfer218 [Edge1,Edge7,Edge18,Edge4,Face12]
  BaseFeature = -> Chamfer218
  Radius = 0.4
FEATURE [Sketcher::SketchObject] Sketch1386
  ExternalGeometry = -> [Fillet165]
  MapMode = 5
  Placement = pos=(0,0,43.1) rot=(0,0,1;0rad)
  Support = -> [Fillet165]
  sketch-geometry (1):
    g0: Circle CenterX=0 CenterY=10.15 CenterZ=0 NormalX=0 NormalY=0 NormalZ=1 AngleXU=0 Radius=3
  constraints (2):
    c: Coincident(g0,g-3)
    c: Radius(g0) = 3
FEATURE [PartDesign::Pocket] Pocket513
  BaseFeature = -> Fillet165
  Length = 5
  Length2 = 100
  Profile = -> Sketch1386
  Type = 0
FEATURE [PartDesign::Body] Body322  label="MG996R008"
  Group = -> [Sketch1387,Pad493,Sketch1463,Pad580,Sketch1371,Pad489,Sketch1399,Pad581,Sketch1381,Pad590,Sketch1374,Pad582,Sketch1396,Pad500,Sketch1405,Pocket519,Sketch1391,Pocket512,Sketch1377,Pad574,Sketch1404,Pocket529,Fillet160,Sketch1407,Pad496,Sketch1373,Pad589,Sketch1383,Pad577,Chamfer218,Fillet165,Sketch1386,Pocket513]
  Origin = -> Origin436
  Tip = -> Pocket513
FEATURE [App::Part] Part115  label="Servo008"
  Group = -> [Body322,Body332,Body307,Body343,Body314]
  Origin = -> Origin439
  Placement = pos=(-47.3841,-8.5,56.9914) rot=(-0.57735,-0.57735,-0.57735;2.0944rad)
FEATURE [Sketcher::SketchObject] Sketch1464
  MapMode = 5
  Placement = pos=(0,0,0) rot=(1,0,0;3.14159rad)
  Support = -> [Pad495]
  sketch-geometry (1):
    g0: Circle CenterX=0 CenterY=0 CenterZ=0 NormalX=0 NormalY=0 NormalZ=1 AngleXU=0 Radius=2.5
  constraints (2):
    c: Coincident(g0,g-1)
    c: Radius(g0) = 2.5
FEATURE [PartDesign::Pocket] Pocket432
  BaseFeature = -> Pad495
  Length = 5
  Length2 = 100
  Profile = -> Sketch1464
  Type = 0
FEATURE [Sketcher::SketchObject] Sketch1460
  MapMode = 5
  Placement = pos=(0,0,0) rot=(1,0,0;3.14159rad)
  Support = -> [Pocket432]
  sketch-geometry (2):
    g0: Circle CenterX=0 CenterY=0 CenterZ=0 NormalX=0 NormalY=0 NormalZ=1 AngleXU=0 Radius=3.5
    g1: Circle CenterX=0 CenterY=0 CenterZ=0 NormalX=0 NormalY=0 NormalZ=1 AngleXU=0 Radius=7
  constraints (4):
    c: Coincident(g0,g-1)
    c: Coincident(g1,g0)
    c: Radius(g0) = 3.5
    c: Radius(g1) = 7
FEATURE [PartDesign::Pocket] Pocket459
  BaseFeature = -> Pocket432
  Length = 0.5
  Length2 = 100
  Profile = -> Sketch1460
  Type = 0
FEATURE [Sketcher::SketchObject] Sketch1455
  MapMode = 5
  Placement = pos=(0,0,5) rot=(0,0,1;0rad)
  Support = -> [Pocket459]
  sketch-geometry (2):
    g0: Circle CenterX=0 CenterY=0 CenterZ=0 NormalX=0 NormalY=0 NormalZ=1 AngleXU=0 Radius=3.5
    g1: Circle CenterX=0 CenterY=0 CenterZ=0 NormalX=0 NormalY=0 NormalZ=1 AngleXU=0 Radius=7
  constraints (4):
    c: Coincident(g0,g-1)
    c: Coincident(g1,g0)
    c: Radius(g0) = 3.5
    c: Radius(g1) = 7
FEATURE [PartDesign::Pocket] Pocket431
  BaseFeature = -> Pocket459
  Length = 0.5
  Length2 = 100
  Profile = -> Sketch1455
  Type = 0
FEATURE [PartDesign::Chamfer] Chamfer244
  Base = -> Pocket431 [Face10,Face2,Face3,Face11]
  BaseFeature = -> Pocket431
  Size = 0.25
FEATURE [PartDesign::Body] Body319
  Group = -> [Sketch1447,Pad495,Sketch1464,Pocket432,Sketch1460,Pocket459,Sketch1455,Pocket431,Chamfer244]
  Origin = -> Origin440
  Tip = -> Chamfer244
FEATURE [App::Part] Part133  label="Ball Bearing002"
  Group = -> [Body319,Body335,Body324]
  Origin = -> Origin413
  Placement = pos=(-144.1,-23.5,26.95) rot=(1,0,0;1.5708rad)
FEATURE [Sketcher::SketchObject] Sketch1466
  ExternalGeometry = -> [Pad492]
  MapMode = 5
  Placement = pos=(0,0,0) rot=(0.57735,0.57735,0.57735;2.0944rad)
  Support = -> [YZ_Plane558]
  sketch-geometry (6):
    g0: LineSegment StartX=-2.67543 StartY=1.2 StartZ=0 EndX=-3.67543 EndY=1.2 EndZ=0
    g1: LineSegment StartX=-3.67543 StartY=1.2 StartZ=0 EndX=-3.67543 EndY=-1.2 EndZ=0
    g2: LineSegment StartX=-3.67543 StartY=-1.2 StartZ=0 EndX=-2.67543 EndY=-1.2 EndZ=0
    g3: LineSegment StartX=-2.67543 StartY=-1.2 StartZ=0 EndX=-3.17543 EndY=-1 EndZ=0
    g4: LineSegment StartX=-3.17543 StartY=-1 StartZ=0 EndX=-3.17543 EndY=1 EndZ=0
    g5: LineSegment StartX=-3.17543 StartY=1 StartZ=0 EndX=-2.67543 EndY=1.2 EndZ=0
  constraints (15):
    c: Horizontal(g0)
    c: Coincident(g0,g1)
    c: Coincident(g1,g2)
    c: Coincident(g2,g3)
    c: Coincident(g3,g4)
    c: Coincident(g4,g5)
    c: Coincident(g5,g0)
    c: Symmetric(g4,g3,g-1)
    c: Symmetric(g0,g2,g-1)
    c: Symmetric(g1,g0,g-1)
    c: DistanceX(g0,g4) = 0.5
    c: DistanceY(g3,g4) = 2
    c: DistanceY(g1,g0) = 2.4
    c: PointOnObject(g3,g-3)
    c: DistanceX(g4,g0) = 0.5
FEATURE [PartDesign::Groove] Groove116  label="M3 Nut Smooth110"
  Angle = 360
  Axis = (-2e-16,3e-16,1)
  Base = (0,0,0)
  BaseFeature = -> Pad492
  Profile = -> Sketch1466
  ReferenceAxis = -> Sketch1466 [V_Axis]
  Reversed = true
FEATURE [PartDesign::Chamfer] Chamfer225  label="M3 Nut Smooth Hole095"
  Base = -> Groove116 [Edge24,Edge23]
  BaseFeature = -> Groove116
  Size = 0.2
FEATURE [PartDesign::Body] Body333  label="M3 Nut058"
  Group = -> [Sketch1462,Pad492,Sketch1466,Groove116,Chamfer225]
  Origin = -> Origin479
  Placement = pos=(-71.6,-9.85,52.05) rot=(0.57735,-0.57735,0.57735;2.0944rad)
  Tip = -> Chamfer225
FEATURE [Sketcher::SketchObject] Sketch1467
  MapMode = 5
  Placement = pos=(130,0,0) rot=(0.57735,0.57735,0.57735;2.0944rad)
  Support = -> [Fillet175]
  sketch-geometry (9):
    g0: LineSegment StartX=30.75 StartY=19.75 StartZ=0 EndX=33.25 EndY=19.75 EndZ=0
    g1: LineSegment StartX=34.5 StartY=18.5 StartZ=0 EndX=34.5 EndY=11.5 EndZ=0
    g2: LineSegment StartX=33.25 StartY=10.25 StartZ=0 EndX=30.75 EndY=10.25 EndZ=0
    g3: LineSegment StartX=29.5 StartY=11.5 StartZ=0 EndX=29.5 EndY=18.5 EndZ=0
    g4: ArcOfCircle CenterX=30.75 CenterY=18.5 CenterZ=0 NormalX=0 NormalY=0 NormalZ=1 AngleXU=0 Radius=1.25 StartAngle=1.5708 EndAngle=3.14159
    g5: ArcOfCircle CenterX=33.25 CenterY=18.5 CenterZ=0 NormalX=0 NormalY=0 NormalZ=1 AngleXU=0 Radius=1.25 StartAngle=1e-16 EndAngle=1.5708
    g6: ArcOfCircle CenterX=33.25 CenterY=11.5 CenterZ=0 NormalX=0 NormalY=0 NormalZ=1 AngleXU=0 Radius=1.25 StartAngle=4.71239 EndAngle=6.28319
    g7: ArcOfCircle CenterX=30.75 CenterY=11.5 CenterZ=0 NormalX=0 NormalY=0 NormalZ=1 AngleXU=0 Radius=1.25 StartAngle=3.14159 EndAngle=4.71239
    g8: Circle [constr] CenterX=32 CenterY=15 CenterZ=0 NormalX=0 NormalY=0 NormalZ=1 AngleXU=0 Radius=2.5
  constraints (23):
    c: Horizontal(g0)
    c: Horizontal(g2)
    c: Vertical(g1)
    c: Vertical(g3)
    c: Tangent(g3,g4) = 1.5708
    c: Tangent(g0,g4) = 1.5708
    c: Tangent(g0,g5) = 1.5708
    c: Tangent(g1,g5) = 1.5708
    c: Tangent(g1,g6) = 1.5708
    c: Tangent(g2,g6) = 1.5708
    c: Tangent(g3,g7) = 1.5708
    c: Tangent(g2,g7) = 1.5708
    c: DistanceY(g2,g0) = 9.5
    c: DistanceX(g3,g1) = 5
    c: Tangent(g8,g3)
    c: Tangent(g8,g1)
    c: Equal(g5,g4)
    c: Equal(g4,g7)
    c: Equal(g7,g6)
    c: Radius(g5) = 1.25
    c: DistanceY(g8,g0) = 4.75
    c: DistanceX(g-1,g8) = 32
    c: DistanceY(g-1,g8) = 15
FEATURE [PartDesign::Pocket] Pocket518  label="Servocable009"
  BaseFeature = -> Fillet175
  Length = 5
  Length2 = 100
  Profile = -> Sketch1467
  Type = 0
FEATURE [Sketcher::SketchObject] Sketch1465
  MapMode = 5
  Placement = pos=(0,0,0) rot=(1,0,0;3.14159rad)
  Support = -> [Pocket518]
  sketch-geometry (4):
    g0: LineSegment StartX=117 StartY=-15 StartZ=0 EndX=125.25 EndY=-15 EndZ=0
    g1: LineSegment StartX=125.25 StartY=-15 StartZ=0 EndX=125.25 EndY=-10 EndZ=0
    g2: LineSegment StartX=125.25 StartY=-10 StartZ=0 EndX=117 EndY=-10 EndZ=0
    g3: LineSegment StartX=117 StartY=-10 StartZ=0 EndX=117 EndY=-15 EndZ=0
  constraints (12):
    c: Coincident(g0,g1)
    c: Coincident(g1,g2)
    c: Coincident(g2,g3)
    c: Coincident(g3,g0)
    c: Horizontal(g0)
    c: Horizontal(g2)
    c: Vertical(g1)
    c: Vertical(g3)
    c: DistanceX(g2,g2) = 8.25
    c: DistanceY(g3,g3) = 5
    c: DistanceY(g2,g-1) = 10
    c: DistanceX(g-1,g2) = 117
FEATURE [PartDesign::Pocket] Pocket526  label="Servopocket Interlock002"
  BaseFeature = -> Pocket518
  Length = 5
  Length2 = 100
  Profile = -> Sketch1465
  Type = 0
FEATURE [PartDesign::Body] Body295  label="Limb_Top_Shell002"
  Group = -> [Sketch1437,Pad481,Pocket438,Pocket445,Sketch1332,SubtractivePipe014,Fillet167,Sketch1435,Pocket435,Sketch1448,Pocket448,Sketch1446,Pocket444,Pad478,Fillet168,Sketch1456,Pocket458,Fillet169,Sketch1335,Pocket517,Sketch1441,Pocket450,Sketch1458,Pocket441,Sketch1440,Pocket443,Sketch1454,Pocket456,Sketch1452,Pocket514,Sketch1461,Pocket454,Sketch1451,Pocket451,Fillet172,Fillet175,Sketch1467,Pocket518,+2 more]
  Origin = -> Origin463
  Placement = pos=(-144.1,-29.45,42.1) rot=(0,0,1;0rad)
  Tip = -> Pocket526
FEATURE [PartDesign::Pad] Pad651  label="M3 Nut Primitive127"
  Length = 1.2
  Length2 = 1.2
  Profile = -> Sketch1393
  Type = 4
FEATURE [Sketcher::SketchObject] Sketch1380
  ExternalGeometry = -> [Pad651]
  MapMode = 5
  Placement = pos=(0,0,0) rot=(0.57735,0.57735,0.57735;2.0944rad)
  Support = -> [YZ_Plane504]
  sketch-geometry (6):
    g0: LineSegment StartX=-2.67543 StartY=1.2 StartZ=0 EndX=-3.67543 EndY=1.2 EndZ=0
    g1: LineSegment StartX=-3.67543 StartY=1.2 StartZ=0 EndX=-3.67543 EndY=-1.2 EndZ=0
    g2: LineSegment StartX=-3.67543 StartY=-1.2 StartZ=0 EndX=-2.67543 EndY=-1.2 EndZ=0
    g3: LineSegment StartX=-2.67543 StartY=-1.2 StartZ=0 EndX=-3.17543 EndY=-1 EndZ=0
    g4: LineSegment StartX=-3.17543 StartY=-1 StartZ=0 EndX=-3.17543 EndY=1 EndZ=0
    g5: LineSegment StartX=-3.17543 StartY=1 StartZ=0 EndX=-2.67543 EndY=1.2 EndZ=0
  constraints (15):
    c: Horizontal(g0)
    c: Coincident(g0,g1)
    c: Coincident(g1,g2)
    c: Coincident(g2,g3)
    c: Coincident(g3,g4)
    c: Coincident(g4,g5)
    c: Coincident(g5,g0)
    c: Symmetric(g4,g3,g-1)
    c: Symmetric(g0,g2,g-1)
    c: Symmetric(g1,g0,g-1)
    c: DistanceX(g0,g4) = 0.5
    c: DistanceY(g3,g4) = 2
    c: DistanceY(g1,g0) = 2.4
    c: PointOnObject(g3,g-3)
    c: DistanceX(g4,g0) = 0.5
FEATURE [PartDesign::Groove] Groove098  label="M3 Nut Smooth094"
  Angle = 360
  Axis = (-2e-16,3e-16,1)
  Base = (0,0,0)
  BaseFeature = -> Pad651
  Profile = -> Sketch1380
  ReferenceAxis = -> Sketch1380 [V_Axis]
  Reversed = true
FEATURE [PartDesign::Chamfer] Chamfer249  label="M3 Nut Smooth Hole105"
  Base = -> Groove098 [Edge24,Edge23]
  BaseFeature = -> Groove098
  Size = 0.2
FEATURE [PartDesign::Body] Body323  label="M3 Nut055"
  Group = -> [Sketch1393,Pad651,Sketch1380,Groove098,Chamfer249]
  Origin = -> Origin488
  Placement = pos=(-23.1,-9.85,52.05) rot=(0.57735,-0.57735,0.57735;2.0944rad)
  Tip = -> Chamfer249
FEATURE [App::Part] Part126  label="Servo Nuts002"
  Group = -> [Body338,Body336,Body333,Body323]
  Origin = -> Origin450
  Placement = pos=(0,17.9,0) rot=(0,0,1;0rad)
FEATURE [PartDesign::Chamfer] Chamfer262  label="M3x20 Smooth047"
  Base = -> Pocket482 [Face11,Edge2,Edge24,Edge3]
  BaseFeature = -> Pocket482
  Size = 0.2
FEATURE [PartDesign::Body] Body316  label="M3x065"
  Group = -> [Sketch1324,Pad536,Sketch1165,Pad522,Sketch1162,Pocket482,Chamfer262]
  Origin = -> Origin447
  Placement = pos=(-149,-30,75) rot=(-1,0,0;1.5708rad)
  Tip = -> Chamfer262
FEATURE [PartDesign::Chamfer] Chamfer263  label="Smooth Pinhead005"
  Base = -> Pad531 [Edge3]
  BaseFeature = -> Pad531
  Size = 0.4
FEATURE [PartDesign::Body] Body347  label="Shoulder_Joint_Ball_Bearing_Pin004"
  Group = -> [Sketch1331,Pad531,Chamfer263]
  Origin = -> Origin504
  Placement = pos=(-115.146,-150.626,71.5546) rot=(-1,0,0;1.5708rad)
  Tip = -> Chamfer263
FEATURE [PartDesign::Chamfer] Chamfer265  label="M3x20 Smooth048"
  Base = -> Pocket500 [Face11,Edge2,Edge24,Edge3]
  BaseFeature = -> Pocket500
  Size = 0.2
FEATURE [PartDesign::Fillet] Fillet177  label="Smooth Servohorn Corners002"
  Base = -> Pocket561 [Edge81,Edge87,Edge82,Edge88,Edge93,Edge94]
  BaseFeature = -> Pocket561
  Radius = 1
FEATURE [Sketcher::SketchObject] Sketch1268
  MapMode = 5
  Placement = pos=(0,0,3) rot=(0,0,1;0rad)
  Support = -> [Fillet177]
  sketch-geometry (13):
    g0: LineSegment [constr] StartX=0 StartY=10.5 StartZ=0 EndX=-9.09327 EndY=5.25 EndZ=0
    g1: LineSegment [constr] StartX=-9.09327 StartY=5.25 StartZ=0 EndX=-9.09327 EndY=-5.25 EndZ=0
    g2: LineSegment [constr] StartX=-9.09327 StartY=-5.25 StartZ=0 EndX=0 EndY=-10.5 EndZ=0
    g3: LineSegment [constr] StartX=0 StartY=-10.5 StartZ=0 EndX=9.09327 EndY=-5.25 EndZ=0
    g4: LineSegment [constr] StartX=9.09327 StartY=-5.25 StartZ=0 EndX=9.09327 EndY=5.25 EndZ=0
    g5: LineSegment [constr] StartX=9.09327 StartY=5.25 StartZ=0 EndX=0 EndY=10.5 EndZ=0
    g6: Circle [constr] CenterX=0 CenterY=0 CenterZ=0 NormalX=0 NormalY=0 NormalZ=1 AngleXU=0 Radius=10.5
    g7: Circle CenterX=0 CenterY=10.5 CenterZ=0 NormalX=0 NormalY=0 NormalZ=1 AngleXU=0 Radius=0.95
    g8: Circle CenterX=9.09327 CenterY=5.25 CenterZ=0 NormalX=0 NormalY=0 NormalZ=1 AngleXU=0 Radius=0.95
    g9: Circle CenterX=9.09327 CenterY=-5.25 CenterZ=0 NormalX=0 NormalY=0 NormalZ=1 AngleXU=0 Radius=0.95
    g10: Circle CenterX=0 CenterY=-10.5 CenterZ=0 NormalX=0 NormalY=0 NormalZ=1 AngleXU=0 Radius=0.95
    g11: Circle CenterX=-9.09327 CenterY=-5.25 CenterZ=0 NormalX=0 NormalY=0 NormalZ=1 AngleXU=0 Radius=0.95
    g12: Circle CenterX=-9.09327 CenterY=5.25 CenterZ=0 NormalX=0 NormalY=0 NormalZ=1 AngleXU=0 Radius=0.95
  constraints (24):
    c: Coincident(g0,g1)
    c: Coincident(g1,g2)
    c: Coincident(g2,g3)
    c: Coincident(g3,g4)
    c: Coincident(g4,g5)
    c: Coincident(g5,g0)
    c: Equal(g0, g1-g5) x5
    c: PointOnObject(g0,g6)
    c: PointOnObject(g1,g6)
    c: PointOnObject(g2,g6)
    c: PointOnObject(g3,g6)
    c: PointOnObject(g4,g6)
    c: PointOnObject(g5,g6)
    c: Coincident(g6,g-1)
    c: PointOnObject(g5,g-2)
    c: Radius(g6) = 10.5
    c: Coincident(g7,g0)
    c: Coincident(g8,g4)
    c: Coincident(g9,g3)
    c: Coincident(g10,g2)
    c: Coincident(g11,g1)
    c: Coincident(g12,g0)
    c: Radius(g12) = 0.95
    c: Equal(g12, g7-g11) x5
FEATURE [PartDesign::Pocket] Pocket554  label="Screwholes Servohorn002"
  BaseFeature = -> Fillet177
  Length = 3
  Length2 = 100
  Profile = -> Sketch1268
  Type = 0
FEATURE [Sketcher::SketchObject] Sketch1250
  MapMode = 5
  Placement = pos=(0,0,0) rot=(1,0,0;3.14159rad)
  Support = -> [Pocket554]
  sketch-geometry (10):
    g0: Circle [constr] CenterX=0 CenterY=0 CenterZ=0 NormalX=0 NormalY=0 NormalZ=1 AngleXU=0 Radius=20
    g1: LineSegment [constr] StartX=-14.1421 StartY=14.1421 StartZ=0 EndX=14.1421 EndY=14.1421 EndZ=0
    g2: LineSegment [constr] StartX=14.1421 StartY=14.1421 StartZ=0 EndX=14.1421 EndY=-14.1421 EndZ=0
    g3: LineSegment [constr] StartX=14.1421 StartY=-14.1421 StartZ=0 EndX=-14.1421 EndY=-14.1421 EndZ=0
    g4: LineSegment [constr] StartX=-14.1421 StartY=-14.1421 StartZ=0 EndX=-14.1421 EndY=14.1421 EndZ=0
    g5: Circle CenterX=-14.1421 CenterY=14.1421 CenterZ=0 NormalX=0 NormalY=0 NormalZ=1 AngleXU=0 Radius=1.2e-15
    g6: Circle CenterX=14.1421 CenterY=14.1421 CenterZ=0 NormalX=0 NormalY=0 NormalZ=1 AngleXU=0 Radius=2.85
    g7: Circle CenterX=14.1421 CenterY=-14.1421 CenterZ=0 NormalX=0 NormalY=0 NormalZ=1 AngleXU=0 Radius=2.85
    g8: Circle CenterX=-14.1421 CenterY=14.1421 CenterZ=0 NormalX=0 NormalY=0 NormalZ=1 AngleXU=0 Radius=2.85
    g9: Circle CenterX=-14.1421 CenterY=-14.1421 CenterZ=0 NormalX=0 NormalY=0 NormalZ=1 AngleXU=0 Radius=2.85
  constraints (24):
    c: Coincident(g0,g-1)
    c: Radius(g0) = 20
    c: Coincident(g1,g2)
    c: Coincident(g2,g3)
    c: Coincident(g3,g4)
    c: Coincident(g4,g1)
    c: Horizontal(g1)
    c: Horizontal(g3)
    c: Vertical(g2)
    c: Vertical(g4)
    c: PointOnObject(g1,g0)
    c: PointOnObject(g2,g0)
    c: PointOnObject(g1,g0)
    c: Equal(g1,g2)
    c: Coincident(g5,g1)
    c: Tangent(g5,g0)
    c: Coincident(g6,g1)
    c: Coincident(g7,g2)
    c: Coincident(g8,g5)
    c: Coincident(g9,g3)
    c: Equal(g9,g8)
    c: Equal(g8,g6)
    c: Equal(g6,g7)
    c: Radius(g6) = 2.85
FEATURE [PartDesign::Pocket] Pocket548  label="Screwheads Mounting002"
  BaseFeature = -> Pocket554
  Length = 8
  Length2 = 100
  Profile = -> Sketch1250
  Type = 0
FEATURE [PartDesign::Chamfer] Chamfer233  label="Screwheads Bottom Chamfer002"
  Base = -> Pocket548 [Edge140,Edge139,Edge138,Edge137]
  BaseFeature = -> Pocket548
  Size = 1.2
FEATURE [PartDesign::Body] Body383  label="Shoulder_Joint_Servohorn_Cap002"
  Group = -> [Sketch1242,Pad644,Sketch1251,Pocket550,Sketch1263,Pocket560,Sketch1428,Pocket553,Sketch1260,Pocket561,Fillet177,Sketch1268,Pocket554,Sketch1250,Pocket548,Chamfer233]
  Origin = -> Origin547
  Tip = -> Chamfer233
FEATURE [PartDesign::Chamfer] Chamfer266  label="M3 Nut Smooth Hole112"
  Base = -> Groove112 [Edge24,Edge23]
  BaseFeature = -> Groove112
  Size = 0.2
FEATURE [PartDesign::Body] Body344  label="M3 Nut062"
  Group = -> [Sketch1284,Pad523,Sketch1294,Groove112,Chamfer266]
  Origin = -> Origin445
  Placement = pos=(-104.661,-159.25,50.9359) rot=(0.862856,-0.357407,0.357407;1.71777rad)
  Tip = -> Chamfer266
FEATURE [PartDesign::Chamfer] Chamfer267
  Base = -> Pad474 [Face7]
  BaseFeature = -> Pad474
  Size = 1.5
FEATURE [PartDesign::Fillet] Fillet157
  Base = -> Chamfer267 [Edge1,Edge7,Edge18,Edge4,Face12]
  BaseFeature = -> Chamfer267
  Radius = 0.4
FEATURE [Sketcher::SketchObject] Sketch1170
  ExternalGeometry = -> [Fillet157]
  MapMode = 5
  Placement = pos=(0,0,43.1) rot=(0,0,1;0rad)
  Support = -> [Fillet157]
  sketch-geometry (1):
    g0: Circle CenterX=0 CenterY=10.15 CenterZ=0 NormalX=0 NormalY=0 NormalZ=1 AngleXU=0 Radius=3
  constraints (2):
    c: Coincident(g0,g-3)
    c: Radius(g0) = 3
FEATURE [PartDesign::Pocket] Pocket430
  BaseFeature = -> Fillet157
  Length = 5
  Length2 = 100
  Profile = -> Sketch1170
  Type = 0
FEATURE [PartDesign::Body] Body325  label="MG996R009"
  Group = -> [Sketch1348,Pad542,Sketch1299,Pad488,Sketch1319,Pad487,Sketch1323,Pad486,Sketch1304,Pad558,Sketch1160,Pad475,Sketch1316,Pad554,Sketch1343,Pocket425,Sketch1301,Pocket505,Sketch1313,Pad482,Sketch1340,Pocket437,Fillet149,Sketch1327,Pad485,Sketch1328,Pad543,Sketch1302,Pad474,Chamfer267,Fillet157,Sketch1170,Pocket430]
  Origin = -> Origin494
  Tip = -> Pocket430
FEATURE [App::Part] Part116  label="Servo009"
  Group = -> [Body325,Body304,Body303,Body379,Body340]
  Origin = -> Origin483
  Placement = pos=(-75.5841,-15.9,113.841) rot=(0.281085,-0.678598,-0.678598;3.68962rad)
FEATURE [PartDesign::Chamfer] Chamfer268  label="M3x20 Smooth049"
  Base = -> Pocket499 [Face11,Edge2,Edge24,Edge3]
  BaseFeature = -> Pocket499
  Size = 0.2
FEATURE [PartDesign::Body] Body377  label="M3x080"
  Group = -> [Sketch1173,Pad535,Sketch1325,Pad559,Sketch1161,Pocket499,Chamfer268]
  Origin = -> Origin433
  Placement = pos=(-121.75,-30,34) rot=(-1,0,0;1.5708rad)
  Tip = -> Chamfer268
FEATURE [PartDesign::Fillet] Fillet178  label="Smooth Edges013"
  Base = -> SubtractivePipe015 [Edge21]
  BaseFeature = -> SubtractivePipe015
  Radius = 1.5
FEATURE [PartDesign::Pocket] Pocket496  label="Screwheads Montage006"
  BaseFeature = -> Fillet178
  Length = 3
  Length2 = 100
  Profile = -> Sketch1172
  Type = 0
FEATURE [Sketcher::SketchObject] Sketch1295
  MapMode = 5
  Placement = pos=(0,0,2) rot=(0,0,1;0rad)
  Support = -> [Pocket496]
  sketch-geometry (3):
    g0: Circle [constr] CenterX=0 CenterY=15 CenterZ=0 NormalX=0 NormalY=0 NormalZ=1 AngleXU=0 Radius=35
    g1: Circle CenterX=-33.541 CenterY=25 CenterZ=0 NormalX=0 NormalY=0 NormalZ=1 AngleXU=0 Radius=1.6
    g2: Circle CenterX=-28.7228 CenterY=35 CenterZ=0 NormalX=0 NormalY=0 NormalZ=1 AngleXU=0 Radius=1.6
  constraints (9):
    c: Radius(g0) = 35
    c: PointOnObject(g1,g0)
    c: PointOnObject(g2,g0)
    c: Equal(g2,g1)
    c: Radius(g2) = 1.6
    c: DistanceY(g1,g2) = 10
    c: DistanceY(g-1,g0) = 15
    c: DistanceY(g0,g1) = 10
    c: DistanceX(g0,g-1) = 0
FEATURE [PartDesign::Pocket] Pocket495  label="Screwholes Montage006"
  BaseFeature = -> Pocket496
  Length = 3
  Length2 = 100
  Profile = -> Sketch1295
  Type = 0
FEATURE [Sketcher::SketchObject] Sketch1300
  MapMode = 5
  Placement = pos=(0,0,5) rot=(0,0,1;0rad)
  Support = -> [Pocket495]
  sketch-geometry (1):
    g0: Circle CenterX=0 CenterY=0 CenterZ=0 NormalX=0 NormalY=0 NormalZ=1 AngleXU=0 Radius=6.15
  constraints (2):
    c: Coincident(g0,g-1)
    c: Radius(g0) = 6.15
FEATURE [PartDesign::Pocket] Pocket474  label="Ball Bearing Flange002"
  BaseFeature = -> Pocket495
  Length = 5
  Length2 = 100
  Profile = -> Sketch1300
  Type = 0
FEATURE [Sketcher::SketchObject] Sketch1303
  MapMode = 5
  Placement = pos=(0,0,0) rot=(1,0,0;3.14159rad)
  Support = -> [Pocket474]
  sketch-geometry (1):
    g0: Circle CenterX=0 CenterY=0 CenterZ=0 NormalX=0 NormalY=0 NormalZ=1 AngleXU=0 Radius=8.15
  constraints (2):
    c: Coincident(g0,g-1)
    c: Radius(g0) = 8.15
FEATURE [PartDesign::Pocket] Pocket464  label="Ball Bearing Pocket002"
  BaseFeature = -> Pocket474
  Length = 4.5
  Length2 = 100
  Profile = -> Sketch1303
  Type = 0
FEATURE [PartDesign::Chamfer] Chamfer269  label="M3 Nut Smooth Hole113"
  Base = -> Groove104 [Edge24,Edge23]
  BaseFeature = -> Groove104
  Size = 0.2
FEATURE [PartDesign::Body] Body309  label="M2 Nut043"
  Group = -> [Sketch1154,Pad517,Sketch1139,Groove104,Chamfer269,Sketch1169,Sketch1145]
  Origin = -> Origin540
  Placement = pos=(0,0,2.75) rot=(0,0,1;0rad)
  Tip = -> Chamfer269
FEATURE [PartDesign::Chamfer] Chamfer270  label="M3x8 Smooth067"
  Base = -> Pocket481 [Face11,Edge2,Edge24,Edge3]
  BaseFeature = -> Pocket481
  Size = 0.2
FEATURE [PartDesign::Body] Body301  label="M2x049"
  Group = -> [Sketch1308,Pad515,Sketch1158,Pad519,Sketch1167,Pocket481,Chamfer270]
  Origin = -> Origin498
  Tip = -> Chamfer270
FEATURE [PartDesign::Chamfer] Chamfer271  label="M3x20 Smooth050"
  Base = -> Pocket516 [Face11,Edge2,Edge24,Edge3]
  BaseFeature = -> Pocket516
  Size = 0.2
FEATURE [PartDesign::Body] Body306  label="M3x064"
  Group = -> [Sketch1422,Pad593,Sketch1409,Pad587,Sketch1388,Pocket516,Chamfer271]
  Origin = -> Origin412
  Placement = pos=(-110.55,-29.35,52.05) rot=(-1,0,0;1.5708rad)
  Tip = -> Chamfer271
FEATURE [App::Part] Part117  label="Shell Screws002"
  Group = -> [Body331,Body306,Body341,Body345]
  Origin = -> Origin551
FEATURE [PartDesign::Fillet] Fillet179  label="Smooth Edges014"
  Base = -> SubtractivePipe013 [Edge20,Edge5]
  BaseFeature = -> SubtractivePipe013
  Radius = 1.5
FEATURE [Sketcher::SketchObject] Sketch1453
  MapMode = 5
  Placement = pos=(0,5,0) rot=(1,0,0;1.5708rad)
  Support = -> [Fillet179]
  sketch-geometry (1):
    g0: Circle CenterX=0 CenterY=0 CenterZ=0 NormalX=0 NormalY=0 NormalZ=1 AngleXU=0 Radius=30
  constraints (2):
    c: Coincident(g0,g-1)
    c: Radius(g0) = 30
FEATURE [PartDesign::Pocket] Pocket447  label="Joint Pan005"
  BaseFeature = -> Fillet179
  Length = 47
  Length2 = 100
  Profile = -> Sketch1453
  Type = 0
FEATURE [Sketcher::SketchObject] Sketch1282
  ExternalGeometry = -> [Pocket447]
  MapMode = 5
  Placement = pos=(0,5,0) rot=(1,0,0;1.5708rad)
  Support = -> [Pocket447]
  sketch-geometry (7):
    g0: ArcOfCircle CenterX=23.5 CenterY=28.2018 CenterZ=0 NormalX=0 NormalY=0 NormalZ=1 AngleXU=0 Radius=1.79818 StartAngle=1.57079 EndAngle=2.66896
    g1: LineSegment StartX=21.8989 StartY=29.0204 StartZ=0 EndX=19.5977 EndY=24.5195 EndZ=0
    g2: ArcOfCircle CenterX=21.1988 CenterY=23.701 CenterZ=0 NormalX=0 NormalY=0 NormalZ=1 AngleXU=0 Radius=1.79818 StartAngle=2.66896 EndAngle=3.98266
    g3: Circle [constr] CenterX=0 CenterY=0 CenterZ=0 NormalX=0 NormalY=0 NormalZ=1 AngleXU=0 Radius=30
    g4: LineSegment StartX=23.5 StartY=30 StartZ=0 EndX=0 EndY=30 EndZ=0
    g5: LineSegment StartX=0 StartY=30 StartZ=0 EndX=0 EndY=22.3607 EndZ=0
    g6: LineSegment StartX=0 StartY=22.3607 StartZ=0 EndX=20 EndY=22.3607 EndZ=0
  constraints (19):
    c: Coincident(g3,g-1)
    c: Radius(g3) = 30
    c: Coincident(g4,g0)
    c: PointOnObject(g4,g3)
    c: Horizontal(g4)
    c: Tangent(g4,g0)
    c: Coincident(g5,g4)
    c: Vertical(g5)
    c: Tangent(g2,g3) = 1.5708
    c: Tangent(g2,g1) = -1.5708
    c: Tangent(g1,g0) = -1.5708
    c: DistanceX(g4,g4) = 23.5
    c: PointOnObject(g4,g-2)
    c: DistanceX(g5,g2) = 20
    c: Equal(g0,g2)
    c: Coincident(g6,g5)
    c: Coincident(g6,g2)
    c: Horizontal(g6)
    c: Horizontal(g-3,g0)
FEATURE [PartDesign::Pocket] Pocket440  label="Shortened Angled Top004"
  BaseFeature = -> Pocket447
  Length = 47
  Length2 = 100
  Profile = -> Sketch1282
  Type = 0
FEATURE [PartDesign::Pocket] Pocket434  label="Servoplacement Helper Pocket004"
  BaseFeature = -> Pocket440
  Length = 15
  Length2 = 100
  Profile = -> Sketch1436
  Type = 0
FEATURE [PartDesign::Pad] Pad473  label="Servoplacement Helper Pad004"
  BaseFeature = -> Pocket434
  Length = 5
  Length2 = 100
  Profile = -> Pocket434 [Face60]
  Type = 0
FEATURE [PartDesign::Fillet] Fillet176  label="Servoplacement Smooth Edges005"
  Base = -> Pad473 [Edge121,Edge125]
  BaseFeature = -> Pad473
  Radius = 0.4
FEATURE [Sketcher::SketchObject] Sketch1434
  MapMode = 5
  Placement = pos=(0,10,-2.2e-15) rot=(1,0,0;1.5708rad)
  Support = -> [Fillet176]
  sketch-geometry (4):
    g0: LineSegment StartX=76.5 StartY=25 StartZ=0 EndX=117 EndY=25 EndZ=0
    g1: LineSegment StartX=117 StartY=25 StartZ=0 EndX=117 EndY=5 EndZ=0
    g2: LineSegment StartX=117 StartY=5 StartZ=0 EndX=76.5 EndY=5 EndZ=0
    g3: LineSegment StartX=76.5 StartY=5 StartZ=0 EndX=76.5 EndY=25 EndZ=0
  constraints (12):
    c: Coincident(g0,g1)
    c: Coincident(g1,g2)
    c: Coincident(g2,g3)
    c: Coincident(g3,g0)
    c: Horizontal(g0)
    c: Horizontal(g2)
    c: Vertical(g1)
    c: Vertical(g3)
    c: DistanceX(g0,g0) = 40.5
    c: DistanceY(g3,g3) = 20
    c: DistanceY(g-1,g2) = 5
    c: DistanceX(g-1,g2) = 76.5
FEATURE [PartDesign::Pocket] Pocket426  label="Servo Pocket008"
  BaseFeature = -> Fillet176
  Length = 30
  Length2 = 100
  Profile = -> Sketch1434
  Type = 0
FEATURE [PartDesign::Fillet] Fillet159  label="Smooth Mount Edges004"
  Base = -> Pocket426 [Edge147,Edge146,Edge141,Edge152]
  BaseFeature = -> Pocket426
  Radius = 0.4
FEATURE [Sketcher::SketchObject] Sketch1333
  MapMode = 5
  Placement = pos=(0,0,30) rot=(0,0,1;0rad)
  Support = -> [Fillet159]
  sketch-geometry (4):
    g0: LineSegment StartX=0 StartY=0 StartZ=0 EndX=130 EndY=0 EndZ=0
    g1: LineSegment StartX=130 StartY=0 StartZ=0 EndX=130 EndY=57 EndZ=0
    g2: LineSegment StartX=130 StartY=57 StartZ=0 EndX=0 EndY=57 EndZ=0
    g3: LineSegment StartX=0 StartY=57 StartZ=0 EndX=0 EndY=0 EndZ=0
  constraints (11):
    c: Coincident(g0,g1)
    c: Coincident(g1,g2)
    c: Coincident(g2,g3)
    c: Coincident(g3,g0)
    c: Horizontal(g0)
    c: Horizontal(g2)
    c: Vertical(g1)
    c: Vertical(g3)
    c: Coincident(g0,g-1)
    c: DistanceY(g1,g1) = 57
    c: DistanceX(g2,g2) = 130
FEATURE [PartDesign::Pocket] Pocket446  label="Remove Top Surface002"
  BaseFeature = -> Fillet159
  Length = 5
  Length2 = 100
  Profile = -> Sketch1333
  Type = 0
FEATURE [Sketcher::SketchObject] Sketch1296
  MapMode = 5
  Placement = pos=(0,0,25) rot=(0,0,1;0rad)
  Support = -> [Pocket446]
  sketch-geometry (7):
    g0: LineSegment StartX=0 StartY=43 StartZ=0 EndX=120 EndY=43 EndZ=0
    g1: ArcOfCircle CenterX=120 CenterY=38 CenterZ=0 NormalX=0 NormalY=0 NormalZ=1 AngleXU=0 Radius=5 StartAngle=3e-16 EndAngle=1.5708
    g2: LineSegment StartX=125 StartY=38 StartZ=0 EndX=125 EndY=10 EndZ=0
    g3: LineSegment StartX=125 StartY=10 StartZ=0 EndX=130 EndY=10 EndZ=0
    g4: LineSegment StartX=130 StartY=10 StartZ=0 EndX=130 EndY=57 EndZ=0
    g5: LineSegment StartX=130 StartY=57 StartZ=0 EndX=0 EndY=57 EndZ=0
    g6: LineSegment StartX=0 StartY=57 StartZ=0 EndX=0 EndY=43 EndZ=0
  constraints (20):
    c: Horizontal(g0)
    c: Tangent(g0,g1) = 1.5708
    c: Tangent(g1,g2) = 1.5708
    c: Coincident(g2,g3)
    c: Horizontal(g3)
    c: Coincident(g3,g4)
    c: Coincident(g4,g5)
    c: Horizontal(g5)
    c: Coincident(g5,g6)
    c: Coincident(g6,g0)
    c: Vertical(g6)
    c: Vertical(g4)
    c: Vertical(g2)
    c: PointOnObject(g0,g-2)
    c: DistanceY(g-1,g5) = 57
    c: DistanceX(g5,g5) = 130
    c: DistanceY(g-1,g3) = 10
    c: DistanceX(g3,g3) = 5
    c: Radius(g1) = 5
    c: DistanceY(g2,g0) = 33
FEATURE [PartDesign::Pocket] Pocket439  label="Remove Shell002"
  BaseFeature = -> Pocket446
  Length = 25
  Length2 = 100
  Profile = -> Sketch1296
  Type = 0
FEATURE [Sketcher::SketchObject] Sketch1443
  MapMode = 5
  Placement = pos=(0,0,25) rot=(0,0,1;0rad)
  Support = -> [Pocket439]
  sketch-geometry (4):
    g0: LineSegment StartX=117 StartY=10 StartZ=0 EndX=125 EndY=10 EndZ=0
    g1: LineSegment StartX=125 StartY=10 StartZ=0 EndX=125 EndY=15 EndZ=0
    g2: LineSegment StartX=125 StartY=15 StartZ=0 EndX=117 EndY=15 EndZ=0
    g3: LineSegment StartX=117 StartY=15 StartZ=0 EndX=117 EndY=10 EndZ=0
  constraints (12):
    c: Coincident(g0,g1)
    c: Coincident(g1,g2)
    c: Coincident(g2,g3)
    c: Coincident(g3,g0)
    c: Horizontal(g0)
    c: Horizontal(g2)
    c: Vertical(g1)
    c: Vertical(g3)
    c: DistanceY(g1,g1) = 5
    c: DistanceX(g2,g2) = 8
    c: DistanceY(g-1,g0) = 10
    c: DistanceX(g-1,g2) = 117
FEATURE [PartDesign::Pocket] Pocket442  label="Remove Shell at Servopocket002"
  BaseFeature = -> Pocket439
  Length = 20
  Length2 = 100
  Profile = -> Sketch1443
  Type = 0
FEATURE [Sketcher::SketchObject] Sketch1286
  MapMode = 5
  Placement = pos=(125,0,0) rot=(0.57735,0.57735,0.57735;2.0944rad)
  Support = -> [Pocket442]
  sketch-geometry (4):
    g0: LineSegment StartX=29.5 StartY=25 StartZ=0 EndX=34.5 EndY=25 EndZ=0
    g1: LineSegment StartX=29.5 StartY=25 StartZ=0 EndX=29.5 EndY=11.5 EndZ=0
    g2: LineSegment StartX=34.5 StartY=25 StartZ=0 EndX=34.5 EndY=11.5 EndZ=0
    g3: ArcOfCircle CenterX=32 CenterY=11.5 CenterZ=0 NormalX=0 NormalY=0 NormalZ=1 AngleXU=0 Radius=2.5 StartAngle=3.14159 EndAngle=6.28319
  constraints (11):
    c: Horizontal(g0)
    c: Coincident(g1,g0)
    c: Vertical(g1)
    c: Coincident(g2,g0)
    c: Vertical(g2)
    c: Tangent(g3,g1) = -1.5708
    c: Tangent(g3,g2) = 1.5708
    c: DistanceX(g0,g0) = 5
    c: DistanceY(g-1,g3) = 11.5
    c: DistanceX(g-1,g3) = 32
    c: DistanceY(g-1,g0) = 25
FEATURE [PartDesign::Pocket] Pocket429  label="Servocable008"
  BaseFeature = -> Pocket442
  Length = 8
  Length2 = 100
  Profile = -> Sketch1286
  Type = 0
FEATURE [Sketcher::SketchObject] Sketch1330
  MapMode = 5
  Placement = pos=(125,0,0) rot=(0.57735,0.57735,0.57735;2.0944rad)
  Support = -> [Pocket429]
  sketch-geometry (8):
    g0: LineSegment StartX=18 StartY=22.9 StartZ=0 EndX=21 EndY=22.9 EndZ=0
    g1: LineSegment StartX=21 StartY=22.9 StartZ=0 EndX=21 EndY=17.1 EndZ=0
    g2: LineSegment StartX=21 StartY=17.1 StartZ=0 EndX=18 EndY=17.1 EndZ=0
    g3: LineSegment StartX=18 StartY=17.1 StartZ=0 EndX=18 EndY=22.9 EndZ=0
    g4: LineSegment StartX=18 StartY=12.9 StartZ=0 EndX=21 EndY=12.9 EndZ=0
    g5: LineSegment StartX=21 StartY=12.9 StartZ=0 EndX=21 EndY=7.1 EndZ=0
    g6: LineSegment StartX=21 StartY=7.1 StartZ=0 EndX=18 EndY=7.1 EndZ=0
    g7: LineSegment StartX=18 StartY=7.1 StartZ=0 EndX=18 EndY=12.9 EndZ=0
  constraints (24):
    c: Coincident(g0,g1)
    c: Coincident(g1,g2)
    c: Coincident(g2,g3)
    c: Coincident(g3,g0)
    c: Horizontal(g0)
    c: Horizontal(g2)
    c: Vertical(g1)
    c: Vertical(g3)
    c: Coincident(g4,g5)
    c: Coincident(g5,g6)
    c: Coincident(g6,g7)
    c: Coincident(g7,g4)
    c: Horizontal(g4)
    c: Horizontal(g6)
    c: Vertical(g5)
    c: Vertical(g7)
    c: Equal(g0,g4)
    c: Equal(g1,g5)
    c: Vertical(g4,g2)
    c: DistanceX(g-1,g6) = 18
    c: DistanceX(g6,g6) = 3
    c: DistanceY(g5,g5) = 5.8
    c: DistanceY(g4,g1) = 4.2
    c: DistanceY(g-1,g6) = 7.1
FEATURE [PartDesign::Pocket] Pocket424  label="Nutholes Servopocket002"
  BaseFeature = -> Pocket429
  Length = 56.5
  Length2 = 100
  Profile = -> Sketch1330
  Type = 0
FEATURE [Sketcher::SketchObject] Sketch1445
  MapMode = 5
  Placement = pos=(0,10,-2.2e-15) rot=(1,0,0;1.5708rad)
  Support = -> [Pocket424]
  sketch-geometry (4):
    g0: Circle CenterX=72.5 CenterY=20 CenterZ=0 NormalX=0 NormalY=0 NormalZ=1 AngleXU=0 Radius=1.6
    g1: Circle CenterX=72.5 CenterY=10 CenterZ=0 NormalX=0 NormalY=0 NormalZ=1 AngleXU=0 Radius=1.6
    g2: Circle CenterX=121 CenterY=20 CenterZ=0 NormalX=0 NormalY=0 NormalZ=1 AngleXU=0 Radius=1.6
    g3: Circle CenterX=121 CenterY=10 CenterZ=0 NormalX=0 NormalY=0 NormalZ=1 AngleXU=0 Radius=1.6
  constraints (12):
    c: Vertical(g3,g2)
    c: Vertical(g1,g0)
    c: Horizontal(g0,g2)
    c: Horizontal(g1,g3)
    c: Equal(g0,g1)
    c: Equal(g1,g2)
    c: Equal(g2,g3)
    c: Radius(g2) = 1.6
    c: DistanceY(g1,g0) = 10
    c: DistanceY(g-1,g1) = 10
    c: DistanceX(g1,g3) = 48.5
    c: DistanceX(g-1,g1) = 72.5
FEATURE [PartDesign::Pocket] Pocket506  label="Screwholes Servopocket005"
  BaseFeature = -> Pocket424
  Length = 18
  Length2 = 100
  Profile = -> Sketch1445
  Type = 0
FEATURE [Sketcher::SketchObject] Sketch1442
  MapMode = 5
  Placement = pos=(0,5,0) rot=(1,0,0;1.5708rad)
  Support = -> [Pocket506]
  sketch-geometry (3):
    g0: Circle [constr] CenterX=0 CenterY=0 CenterZ=0 NormalX=0 NormalY=0 NormalZ=1 AngleXU=0 Radius=35
    g1: Circle CenterX=33.541 CenterY=10 CenterZ=0 NormalX=0 NormalY=0 NormalZ=1 AngleXU=0 Radius=1.6
    g2: Circle CenterX=28.7228 CenterY=20 CenterZ=0 NormalX=0 NormalY=0 NormalZ=1 AngleXU=0 Radius=1.6
  constraints (8):
    c: Coincident(g0,g-1)
    c: Radius(g0) = 35
    c: PointOnObject(g1,g0)
    c: PointOnObject(g2,g0)
    c: Equal(g2,g1)
    c: Radius(g2) = 1.6
    c: DistanceY(g1,g2) = 10
    c: DistanceY(g-1,g1) = 10
FEATURE [PartDesign::Pocket] Pocket427  label="Screwholes Servohorn Mount004"
  BaseFeature = -> Pocket506
  Length = 20
  Length2 = 100
  Profile = -> Sketch1442
  Type = 0
FEATURE [Sketcher::SketchObject] Sketch1279
  MapMode = 5
  Placement = pos=(0,43,0) rot=(0,0.707107,0.707107;3.14159rad)
  Support = -> [Pocket427]
  sketch-geometry (3):
    g0: Circle [constr] CenterX=0 CenterY=0 CenterZ=0 NormalX=0 NormalY=0 NormalZ=1 AngleXU=0 Radius=35
    g1: Circle CenterX=-33.541 CenterY=10 CenterZ=0 NormalX=0 NormalY=0 NormalZ=1 AngleXU=0 Radius=1.6
    g2: Circle CenterX=-28.7228 CenterY=20 CenterZ=0 NormalX=0 NormalY=0 NormalZ=1 AngleXU=0 Radius=1.6
  constraints (8):
    c: Coincident(g0,g-1)
    c: Radius(g0) = 35
    c: PointOnObject(g1,g0)
    c: PointOnObject(g2,g0)
    c: Equal(g2,g1)
    c: Radius(g2) = 1.6
    c: DistanceY(g1,g2) = 10
    c: DistanceY(g-1,g1) = 10
FEATURE [PartDesign::Pocket] Pocket428  label="Screwholes Ball Bearing Mount002"
  BaseFeature = -> Pocket427
  Length = 10
  Length2 = 100
  Profile = -> Sketch1279
  Type = 0
FEATURE [Sketcher::SketchObject] Sketch1292
  MapMode = 5
  Placement = pos=(0,0,25) rot=(0,0,1;0rad)
  Support = -> [Pocket428]
  sketch-geometry (6):
    g0: LineSegment StartX=0 StartY=14 StartZ=0 EndX=40 EndY=14 EndZ=0
    g1: LineSegment StartX=40 StartY=14 StartZ=0 EndX=40 EndY=26 EndZ=0
    g2: LineSegment StartX=0 StartY=31 StartZ=0 EndX=0 EndY=14 EndZ=0
    g3: LineSegment StartX=40 StartY=26 StartZ=0 EndX=67.5 EndY=26 EndZ=0
    g4: LineSegment StartX=67.5 StartY=26 StartZ=0 EndX=67.5 EndY=31 EndZ=0
    g5: LineSegment StartX=67.5 StartY=31 StartZ=0 EndX=0 EndY=31 EndZ=0
  constraints (18):
    c: Coincident(g0,g1)
    c: Coincident(g2,g0)
    c: Horizontal(g0)
    c: Vertical(g1)
    c: Vertical(g2)
    c: PointOnObject(g0,g-2)
    c: DistanceY(g1,g2) = 17
    c: DistanceY(g-1,g0) = 14
    c: Horizontal(g3)
    c: Coincident(g4,g3)
    c: Vertical(g4)
    c: Horizontal(g5)
    c: Coincident(g4,g5)
    c: Coincident(g1,g3)
    c: Coincident(g5,g2)
    c: DistanceX(g-1,g4) = 67.5
    c: DistanceY(g4,g4) = 5
    c: DistanceX(g0,g0) = 40
FEATURE [PartDesign::Pocket] Pocket493  label="Interlock002"
  BaseFeature = -> Pocket428
  Length = 20
  Length2 = 100
  Profile = -> Sketch1292
  Type = 0
FEATURE [PartDesign::Pocket] Pocket453  label="Bottom Nuthole Ball Bearing Mount002"
  BaseFeature = -> Pocket493
  Length = 38
  Length2 = 100
  Profile = -> Sketch1290
  Reversed = true
  Type = 0
FEATURE [PartDesign::Pocket] Pocket436  label="Top Nuthole Ball Bearing Mount002"
  BaseFeature = -> Pocket453
  Length = 33
  Length2 = 100
  Profile = -> Sketch1444
  Reversed = true
  Type = 0
FEATURE [PartDesign::Fillet] Fillet154  label="Smooth Interlock004"
  Base = -> Pocket436 [Edge21,Edge15,Edge85,Edge118,Edge117,Edge116,Edge75,Edge13,Edge76,Edge178,Edge179,Edge88,Edge84,Edge83,Edge82,Edge81,Edge14,Edge72,Edge78,Edge87,Edge86]
  BaseFeature = -> Pocket436
  Radius = 0.4
FEATURE [PartDesign::Fillet] Fillet150  label="Smooth Servopocket002"
  Base = -> Fillet154 [Edge244,Edge256,Edge257,Edge246,Edge255]
  BaseFeature = -> Fillet154
  Radius = 1
FEATURE [PartDesign::Chamfer] Chamfer272  label="M3 Nut Smooth Hole114"
  Base = -> Groove110 [Edge24,Edge23]
  BaseFeature = -> Groove110
  Size = 0.2
FEATURE [PartDesign::Body] Body346  label="M3 Nut063"
  Group = -> [Sketch1317,Pad557,Sketch1347,Groove110,Chamfer272]
  Origin = -> Origin421
  Placement = pos=(-138.956,-159.25,84.9639) rot=(0.862856,-0.357407,0.357407;1.71777rad)
  Tip = -> Chamfer272
FEATURE [PartDesign::Chamfer] Chamfer273  label="M3x8 Smooth068"
  Base = -> Pocket469 [Face11,Edge2,Edge24,Edge3]
  BaseFeature = -> Pocket469
  Size = 0.2
FEATURE [PartDesign::Body] Body312  label="M2x051"
  Group = -> [Sketch1146,Pad491,Sketch1144,Pad502,Sketch1150,Pocket469,Chamfer273]
  Origin = -> Origin557
  Tip = -> Chamfer273
FEATURE [PartDesign::Chamfer] Chamfer274  label="M3x8 Smooth069"
  Base = -> Pocket540 [Face11,Edge2,Edge24,Edge3]
  BaseFeature = -> Pocket540
  Size = 0.2
FEATURE [PartDesign::Body] Body388  label="M2x059"
  Group = -> [Sketch1253,Pad598,Sketch1228,Pad612,Sketch1254,Pocket540,Chamfer274]
  Origin = -> Origin536
  Tip = -> Chamfer274
FEATURE [App::Part] Part146  label="M045"
  Group = -> [Body388,Body342]
  Origin = -> Origin567
  Placement = pos=(-9.8e-15,10.5,80) rot=(0,1,0;3.14159rad)
FEATURE [PartDesign::Chamfer] Chamfer275  label="M3 Nut Smooth Hole115"
  Base = -> Groove108 [Edge24,Edge23]
  BaseFeature = -> Groove108
  Size = 0.2
FEATURE [PartDesign::Body] Body330  label="M3 Nut057"
  Group = -> [Sketch1285,Pad525,Sketch1287,Groove108,Chamfer275]
  Origin = -> Origin473
  Placement = pos=(-111.697,-159.25,43.8385) rot=(0.862856,-0.357407,0.357407;1.71777rad)
  Tip = -> Chamfer275
FEATURE [PartDesign::Chamfer] Chamfer276  label="M3x20 Smooth051"
  Base = -> Pocket507 [Face11,Edge2,Edge24,Edge3]
  BaseFeature = -> Pocket507
  Size = 0.2
FEATURE [PartDesign::Body] Body385  label="M3x083"
  Group = -> [Sketch1318,Pad534,Sketch1334,Pad550,Sketch1339,Pocket507,Chamfer276]
  Origin = -> Origin499
  Placement = pos=(-156,-30,68) rot=(-1,0,0;1.5708rad)
  Tip = -> Chamfer276
FEATURE [PartDesign::Chamfer] Chamfer277  label="M3 Nut Smooth Hole116"
  Base = -> Groove133 [Edge24,Edge23]
  BaseFeature = -> Groove133
  Size = 0.2
FEATURE [PartDesign::Body] Body380  label="M3 Nut069"
  Group = -> [Sketch1223,Pad645,Sketch1215,Groove133,Chamfer277]
  Origin = -> Origin511
  Placement = pos=(1.5e-14,-55.6,176.35) rot=(0.57735,-0.57735,0.57735;4.18879rad)
  Tip = -> Chamfer277
FEATURE [PartDesign::Chamfer] Chamfer278  label="M3x8 Smooth070"
  Base = -> Pocket466 [Face11,Edge2,Edge24,Edge3]
  BaseFeature = -> Pocket466
  Size = 0.2
FEATURE [PartDesign::Body] Body387  label="M2x058"
  Group = -> [Sketch1155,Pad524,Sketch1152,Pad509,Sketch1164,Pocket466,Chamfer278]
  Origin = -> Origin543
  Tip = -> Chamfer278
FEATURE [App::Part] Part134  label="M039"
  Group = -> [Body387,Body309]
  Origin = -> Origin553
  Placement = pos=(9.1,5.25,80) rot=(0,1,0;3.14159rad)
FEATURE [PartDesign::Fillet] Fillet181  label="Servocable Smooth Edges002"
  Base = -> Pocket485 [Edge48,Edge43]
  BaseFeature = -> Pocket485
  Radius = 0.5
FEATURE [Sketcher::SketchObject] Sketch1365
  MapMode = 5
  Placement = pos=(0,-22,0) rot=(1,0,0;1.5708rad)
  Support = -> [Fillet181]
  sketch-geometry (1):
    g0: Circle CenterX=38.25 CenterY=15 CenterZ=0 NormalX=0 NormalY=0 NormalZ=1 AngleXU=0 Radius=0.95
  constraints (3):
    c: DistanceY(g-1,g0) = 15
    c: DistanceX(g-1,g0) = 38.25
    c: Radius(g0) = 0.95
FEATURE [PartDesign::Pocket] Pocket486  label="Ball Bearing Pin Screwhole002"
  BaseFeature = -> Fillet181
  Length = 3
  Length2 = 100
  Profile = -> Sketch1365
  Type = 0
FEATURE [Sketcher::SketchObject] Sketch1275
  ExternalGeometry = -> [Pocket486]
  MapMode = 5
  Placement = pos=(0,-19,0) rot=(0,0.707107,0.707107;3.14159rad)
  Support = -> [Pocket486]
  sketch-geometry (7):
    g0: LineSegment StartX=-36.2 StartY=16.1836 StartZ=0 EndX=-38.25 EndY=17.3671 EndZ=0
    g1: LineSegment StartX=-38.25 StartY=17.3671 StartZ=0 EndX=-40.3 EndY=16.1836 EndZ=0
    g2: LineSegment StartX=-40.3 StartY=16.1836 StartZ=0 EndX=-40.3 EndY=13.8164 EndZ=0
    g3: LineSegment StartX=-40.3 StartY=13.8164 StartZ=0 EndX=-38.25 EndY=12.6329 EndZ=0
    g4: LineSegment StartX=-38.25 StartY=12.6329 StartZ=0 EndX=-36.2 EndY=13.8164 EndZ=0
    g5: LineSegment StartX=-36.2 StartY=13.8164 StartZ=0 EndX=-36.2 EndY=16.1836 EndZ=0
    g6: Circle [constr] CenterX=-38.25 CenterY=15 CenterZ=0 NormalX=0 NormalY=0 NormalZ=1 AngleXU=0 Radius=2.36714
  constraints (16):
    c: Coincident(g0,g1)
    c: Coincident(g1,g2)
    c: Coincident(g2,g3)
    c: Coincident(g3,g4)
    c: Coincident(g4,g5)
    c: Coincident(g5,g0)
    c: Equal(g0, g1-g5) x5
    c: PointOnObject(g0,g6)
    c: PointOnObject(g1,g6)
    c: PointOnObject(g2,g6)
    c: PointOnObject(g3,g6)
    c: PointOnObject(g4,g6)
    c: PointOnObject(g5,g6)
    c: Coincident(g6,g-3)
    c: Vertical(g5)
    c: DistanceX(g1,g0) = 4.1
FEATURE [PartDesign::Pocket] Pocket492  label="Ball Bearing Pin Nuthole002"
  BaseFeature = -> Pocket486
  Length = 1.5
  Length2 = 100
  Profile = -> Sketch1275
  Type = 0
FEATURE [PartDesign::Fillet] Fillet180  label="Smooth Counterpart Corner002"
  Base = -> Pocket492 [Edge3]
  BaseFeature = -> Pocket492
  Radius = 5
FEATURE [PartDesign::Chamfer] Chamfer279  label="M3 Nut Smooth Hole117"
  Base = -> Groove107 [Edge24,Edge23]
  BaseFeature = -> Groove107
  Size = 0.2
FEATURE [PartDesign::Body] Body300  label="M2 Nut041"
  Group = -> [Sketch1142,Pad528,Sketch1307,Groove107,Chamfer279,Sketch1311,Sketch1310]
  Origin = -> Origin572
  Placement = pos=(0,0,2.75) rot=(0,0,1;0rad)
  Tip = -> Chamfer279
FEATURE [App::Part] Part127  label="M038"
  Group = -> [Body301,Body300]
  Origin = -> Origin431
  Placement = pos=(-9.1,5.25,80) rot=(0,1,0;3.14159rad)
FEATURE [PartDesign::Chamfer] Chamfer280  label="M3x8 Smooth071"
  Base = -> Pocket467 [Face11,Edge2,Edge24,Edge3]
  BaseFeature = -> Pocket467
  Size = 0.2
FEATURE [PartDesign::Body] Body298  label="M2x048"
  Group = -> [Sketch1159,Pad501,Sketch1143,Pad512,Sketch1147,Pocket467,Chamfer280]
  Origin = -> Origin560
  Tip = -> Chamfer280
FEATURE [PartDesign::Fillet] Fillet182  label="Smooth Servo Pocket002"
  Base = -> Fillet180 [Edge80,Edge77,Edge76,Edge79,Edge95]
  BaseFeature = -> Fillet180
  Radius = 1
FEATURE [Sketcher::SketchObject] Sketch1283
  MapMode = 5
  Placement = pos=(0,0,0) rot=(0,0.707107,0.707107;3.14159rad)
  Support = -> [Fillet182]
  sketch-geometry (4):
    g0: LineSegment StartX=0 StartY=0 StartZ=0 EndX=-56.5 EndY=0 EndZ=0
    g1: LineSegment StartX=-56.5 StartY=0 StartZ=0 EndX=-56.5 EndY=5 EndZ=0
    g2: LineSegment StartX=-56.5 StartY=5 StartZ=0 EndX=0 EndY=5 EndZ=0
    g3: LineSegment StartX=0 StartY=5 StartZ=0 EndX=0 EndY=0 EndZ=0
  constraints (11):
    c: Coincident(g0,g1)
    c: Coincident(g1,g2)
    c: Coincident(g2,g3)
    c: Coincident(g3,g0)
    c: Horizontal(g0)
    c: Horizontal(g2)
    c: Vertical(g1)
    c: Vertical(g3)
    c: Coincident(g0,g-1)
    c: DistanceY(g1,g1) = 5
    c: DistanceX(g2,g2) = 56.5
FEATURE [PartDesign::Pad] Pad546  label="Elongate Baseplate002"
  BaseFeature = -> Fillet182
  Length = 10
  Length2 = 100
  Profile = -> Sketch1283
  Type = 0
FEATURE [PartDesign::Fillet] Fillet146  label="Smooth Edges011"
  Base = -> Pad546 [Edge135,Edge159]
  BaseFeature = -> Pad546
  Radius = 0.4
FEATURE [PartDesign::Body] Body296  label="Wrist_Counterpart002"
  Group = -> [Sketch1277,Pad532,Sketch1288,Pocket497,Sketch1274,Pocket480,Sketch1280,Pocket461,Sketch1281,Pocket501,Sketch1369,Pocket485,Fillet181,Sketch1365,Pocket486,Sketch1275,Pocket492,Fillet180,Fillet182,Sketch1283,Pad546,Fillet146]
  Origin = -> Origin446
  Placement = pos=(-115.966,-155,33.9411) rot=(0.382683,0,0.92388;3.14159rad)
  Tip = -> Fillet146
FEATURE [PartDesign::Fillet] Fillet183  label="Smooth Servocable Edges006"
  Base = -> Fillet150 [Edge10,Edge199]
  BaseFeature = -> Fillet150
  Radius = 2.5
FEATURE [PartDesign::Fillet] Fillet184
  Base = -> Pad511 [Face5,Edge96,Face4]
  BaseFeature = -> Pad511
  Radius = 0.2
FEATURE [PartDesign::Body] Body310  label="Futuba FSH6B006"
  Group = -> [Sketch1117,Pad503,Sketch1119,Pocket455,Sketch1122,Pocket460,Sketch1128,Pocket452,Sketch1127,Pad511,Fillet184]
  Origin = -> Origin428
  Tip = -> Fillet184
FEATURE [App::Part] Part143  label="Servohorn010"
  Group = -> [Body310]
  Origin = -> Origin514
  Placement = pos=(0,-6.5e-15,-50.4) rot=(1,0,0;3.14159rad)
FEATURE [PartDesign::Fillet] Fillet185
  Base = -> Pocket557 [Edge26,Edge27,Edge72,Edge63,Edge70,Edge78,Edge51,Edge49,Edge71,Edge50,Edge79,Edge86,Edge30,Edge21,Edge4,Edge29,Edge105,Edge107,Edge109,Edge111,Edge113,Edge114,Edge123]
  BaseFeature = -> Pocket557
  Radius = 0.4
FEATURE [Sketcher::SketchObject] Sketch1204
  MapMode = 5
  Placement = pos=(0,20.15,0) rot=(0,0.707107,0.707107;3.14159rad)
  Support = -> [Fillet185]
  sketch-geometry (4):
    g0: LineSegment StartX=-3.25 StartY=2 StartZ=0 EndX=3.25 EndY=2 EndZ=0
    g1: LineSegment StartX=3.25 StartY=2 StartZ=0 EndX=3.25 EndY=6 EndZ=0
    g2: LineSegment StartX=3.25 StartY=6 StartZ=0 EndX=-3.25 EndY=6 EndZ=0
    g3: LineSegment StartX=-3.25 StartY=6 StartZ=0 EndX=-3.25 EndY=2 EndZ=0
  constraints (11):
    c: Coincident(g0,g1)
    c: Coincident(g1,g2)
    c: Coincident(g2,g3)
    c: Coincident(g3,g0)
    c: Horizontal(g0)
    c: Vertical(g1)
    c: Vertical(g3)
    c: DistanceY(g-1,g0) = 2
    c: DistanceY(g1,g1) = 4
    c: Symmetric(g2,g1,g-2)
    c: DistanceX(g2,g2) = 6.5
FEATURE [PartDesign::Pad] Pad561
  BaseFeature = -> Fillet185
  Length = 1
  Length2 = 100
  Profile = -> Sketch1204
  Type = 0
FEATURE [Sketcher::SketchObject] Sketch1190
  MapMode = 5
  Placement = pos=(0,21.15,0) rot=(0,0.707107,0.707107;3.14159rad)
  Support = -> [Pad561]
  sketch-geometry (4):
    g0: LineSegment StartX=-2.75 StartY=5.5 StartZ=0 EndX=2.75 EndY=5.5 EndZ=0
    g1: LineSegment StartX=2.75 StartY=5.5 StartZ=0 EndX=2.75 EndY=2.5 EndZ=0
    g2: LineSegment StartX=2.75 StartY=2.5 StartZ=0 EndX=-2.75 EndY=2.5 EndZ=0
    g3: LineSegment StartX=-2.75 StartY=2.5 StartZ=0 EndX=-2.75 EndY=5.5 EndZ=0
  constraints (11):
    c: Coincident(g0,g1)
    c: Coincident(g1,g2)
    c: Coincident(g2,g3)
    c: Coincident(g3,g0)
    c: Horizontal(g0)
    c: Vertical(g1)
    c: Vertical(g3)
    c: Symmetric(g1,g2,g-2)
    c: DistanceY(g1,g0) = 3
    c: DistanceY(g-1,g1) = 2.5
    c: DistanceX(g0,g0) = 5.5
FEATURE [PartDesign::Pad] Pad642
  BaseFeature = -> Pad561
  Length = 4
  Length2 = 100
  Profile = -> Sketch1190
  Type = 0
FEATURE [Sketcher::SketchObject] Sketch1222
  MapMode = 5
  Placement = pos=(0,0,0) rot=(1,0,0;3.14159rad)
  Support = -> [Pad642]
  sketch-geometry (4):
    g0: LineSegment StartX=-10 StartY=-20.15 StartZ=0 EndX=10 EndY=-20.15 EndZ=0
    g1: LineSegment StartX=10 StartY=-20.15 StartZ=0 EndX=10 EndY=20.15 EndZ=0
    g2: LineSegment StartX=10 StartY=20.15 StartZ=0 EndX=-10 EndY=20.15 EndZ=0
    g3: LineSegment StartX=-10 StartY=20.15 StartZ=0 EndX=-10 EndY=-20.15 EndZ=0
  constraints (10):
    c: Coincident(g0,g1)
    c: Coincident(g1,g2)
    c: Coincident(g2,g3)
    c: Coincident(g3,g0)
    c: Horizontal(g0)
    c: Vertical(g1)
    c: Symmetric(g2,g1,g-2)
    c: Symmetric(g0,g2,g-1)
    c: DistanceX(g2,g2) = 20
    c: DistanceY(g1,g1) = 40.3
FEATURE [PartDesign::Pad] Pad551
  BaseFeature = -> Pad642
  Length = 2
  Length2 = 100
  Profile = -> Sketch1222
  Type = 0
FEATURE [PartDesign::Chamfer] Chamfer230
  Base = -> Pad551 [Face7]
  BaseFeature = -> Pad551
  Size = 1.5
FEATURE [PartDesign::Fillet] Fillet153
  Base = -> Chamfer230 [Edge1,Edge7,Edge18,Edge4,Face12]
  BaseFeature = -> Chamfer230
  Radius = 0.4
FEATURE [Sketcher::SketchObject] Sketch1198
  ExternalGeometry = -> [Fillet153]
  MapMode = 5
  Placement = pos=(0,0,43.1) rot=(0,0,1;0rad)
  Support = -> [Fillet153]
  sketch-geometry (1):
    g0: Circle CenterX=0 CenterY=10.15 CenterZ=0 NormalX=0 NormalY=0 NormalZ=1 AngleXU=0 Radius=3
  constraints (2):
    c: Coincident(g0,g-3)
    c: Radius(g0) = 3
FEATURE [PartDesign::Pocket] Pocket503
  BaseFeature = -> Fillet153
  Length = 5
  Length2 = 100
  Profile = -> Sketch1198
  Type = 0
FEATURE [PartDesign::Body] Body367  label="MG996R010"
  Group = -> [Sketch1196,Pad547,Sketch1208,Pad575,Sketch1195,Pad649,Sketch1202,Pad640,Sketch1206,Pad548,Sketch1188,Pad565,Sketch1207,Pad560,Sketch1212,Pocket556,Sketch1177,Pocket564,Sketch1225,Pad646,Sketch1265,Pocket557,Fillet185,Sketch1204,Pad561,Sketch1190,Pad642,Sketch1222,Pad551,Chamfer230,Fillet153,Sketch1198,Pocket503]
  Origin = -> Origin521
  Tip = -> Pocket503
FEATURE [PartDesign::Chamfer] Chamfer281  label="M3 Nut Smooth Hole118"
  Base = -> Groove113 [Edge24,Edge23]
  BaseFeature = -> Groove113
  Size = 0.2
FEATURE [PartDesign::Body] Body329  label="M3 Nut056"
  Group = -> [Sketch1293,Pad539,Sketch1346,Groove113,Chamfer281]
  Origin = -> Origin475
  Placement = pos=(-146.027,-159.25,78.1297) rot=(0.862856,-0.357407,0.357407;1.71777rad)
  Tip = -> Chamfer281
FEATURE [PartDesign::Chamfer] Chamfer282  label="M3 Nut Smooth Hole119"
  Base = -> Groove099 [Edge24,Edge23]
  BaseFeature = -> Groove099
  Size = 0.2
FEATURE [PartDesign::Body] Body321  label="M2 Nut046"
  Group = -> [Sketch1148,Pad508,Sketch1168,Groove099,Chamfer282,Sketch1309,Sketch1166]
  Origin = -> Origin518
  Placement = pos=(0,0,2.75) rot=(0,0,1;0rad)
  Tip = -> Chamfer282
FEATURE [App::Part] Part142  label="M044"
  Group = -> [Body298,Body321]
  Origin = -> Origin524
  Placement = pos=(9.1,-5.25,80) rot=(0,1,0;3.14159rad)
FEATURE [PartDesign::Chamfer] Chamfer283  label="M3 Nut Smooth Hole120"
  Base = -> Groove101 [Edge24,Edge23]
  BaseFeature = -> Groove101
  Size = 0.2
FEATURE [PartDesign::Body] Body313  label="M2 Nut044"
  Group = -> [Sketch1156,Pad505,Sketch1138,Groove101,Chamfer283,Sketch1136,Sketch1137]
  Origin = -> Origin532
  Placement = pos=(0,0,2.75) rot=(0,0,1;0rad)
  Tip = -> Chamfer283
FEATURE [App::Part] Part141  label="M043"
  Group = -> [Body312,Body313]
  Origin = -> Origin558
  Placement = pos=(-9.8e-15,-10.5,80) rot=(0,1,0;3.14159rad)
FEATURE [PartDesign::Fillet] Fillet187  label="Smooth Servo Pocket Edges002"
  Base = -> Pocket545 [Edge62,Edge137,Edge61,Edge146,Edge60]
  BaseFeature = -> Pocket545
  Radius = 1
FEATURE [PartDesign::Fillet] Fillet152  label="Smooth Servocable Edges005"
  Base = -> Fillet187 [Edge10,Edge165]
  BaseFeature = -> Fillet187
  Radius = 2.5
FEATURE [PartDesign::Fillet] Fillet188  label="Smooth Edges015"
  Base = -> SubtractivePipe011 [Edge21]
  BaseFeature = -> SubtractivePipe011
  Radius = 1.5
FEATURE [Sketcher::SketchObject] Sketch1124
  MapMode = 5
  Placement = pos=(0,0,5) rot=(0,0,1;0rad)
  Support = -> [Fillet188]
  sketch-geometry (33):
    g0: LineSegment [constr] StartX=11.6913 StartY=6.75 StartZ=0 EndX=0 EndY=13.5 EndZ=0
    g1: LineSegment [constr] StartX=0 StartY=13.5 StartZ=0 EndX=-11.6913 EndY=6.75 EndZ=0
    g2: LineSegment [constr] StartX=-11.6913 StartY=6.75 StartZ=0 EndX=-11.6913 EndY=-6.75 EndZ=0
    g3: LineSegment [constr] StartX=-11.6913 StartY=-6.75 StartZ=0 EndX=0 EndY=-13.5 EndZ=0
    g4: LineSegment [constr] StartX=-6e-16 StartY=-13.5 StartZ=0 EndX=11.6913 EndY=-6.75 EndZ=0
    g5: LineSegment [constr] StartX=11.6913 StartY=-6.75 StartZ=0 EndX=11.6913 EndY=6.75 EndZ=0
    g6: Circle [constr] CenterX=0 CenterY=0 CenterZ=0 NormalX=0 NormalY=0 NormalZ=1 AngleXU=0 Radius=13.5
    g7: LineSegment [constr] StartX=7.5 StartY=9e-16 StartZ=0 EndX=3.75 EndY=6.49519 EndZ=0
    g8: LineSegment [constr] StartX=3.75 StartY=6.49519 StartZ=0 EndX=-3.75 EndY=6.49519 EndZ=0
    g9: LineSegment [constr] StartX=-3.75 StartY=6.49519 StartZ=0 EndX=-7.5 EndY=-9e-16 EndZ=0
    g10: LineSegment [constr] StartX=-7.5 StartY=-9e-16 StartZ=0 EndX=-3.75 EndY=-6.49519 EndZ=0
    g11: LineSegment [constr] StartX=-3.75 StartY=-6.49519 StartZ=0 EndX=3.75 EndY=-6.49519 EndZ=0
    g12: LineSegment [constr] StartX=3.75 StartY=-6.49519 StartZ=0 EndX=7.5 EndY=9e-16 EndZ=0
    g13: Circle [constr] CenterX=0 CenterY=0 CenterZ=0 NormalX=0 NormalY=0 NormalZ=1 AngleXU=0 Radius=7.5
    g14: ArcOfCircle CenterX=11.6913 CenterY=-6.75 CenterZ=0 NormalX=0 NormalY=0 NormalZ=1 AngleXU=0 Radius=2.6 StartAngle=4.34694 EndAngle=7.17223
    g15: ArcOfCircle CenterX=-6e-16 CenterY=-13.5 CenterZ=0 NormalX=0 NormalY=0 NormalZ=1 AngleXU=0 Radius=2.6 StartAngle=3.29974 EndAngle=6.12503
    g16: ArcOfCircle CenterX=-11.6913 CenterY=-6.75 CenterZ=0 NormalX=0 NormalY=0 NormalZ=1 AngleXU=0 Radius=2.6 StartAngle=2.25255 EndAngle=5.07784
    g17: ArcOfCircle CenterX=-11.6913 CenterY=6.75 CenterZ=0 NormalX=0 NormalY=0 NormalZ=1 AngleXU=0 Radius=2.6 StartAngle=1.20535 EndAngle=4.03064
    g18: ArcOfCircle CenterX=0 CenterY=13.5 CenterZ=0 NormalX=0 NormalY=0 NormalZ=1 AngleXU=0 Radius=2.6 StartAngle=0.15815 EndAngle=2.98344
    g19: ArcOfCircle CenterX=11.6913 CenterY=6.75 CenterZ=0 NormalX=0 NormalY=0 NormalZ=1 AngleXU=0 Radius=2.6 StartAngle=5.39414 EndAngle=8.21943
    g20: LineSegment StartX=13.3297 StartY=4.73117 StartZ=0 EndX=7.5 EndY=9e-16 EndZ=0
    g21: LineSegment StartX=7.5 StartY=9e-16 StartZ=0 EndX=13.3297 EndY=-4.73117 EndZ=0
    g22: LineSegment StartX=10.7622 StartY=-9.17831 StartZ=0 EndX=3.75 EndY=-6.49519 EndZ=0
    g23: LineSegment StartX=3.75 StartY=-6.49519 StartZ=0 EndX=2.56755 EndY=-13.9095 EndZ=0
    g24: LineSegment StartX=-2.56755 StartY=-13.9095 StartZ=0 EndX=-3.75 EndY=-6.49519 EndZ=0
    g25: LineSegment StartX=-3.75 StartY=-6.49519 StartZ=0 EndX=-10.7622 EndY=-9.17831 EndZ=0
    g26: LineSegment StartX=-13.3297 StartY=-4.73117 StartZ=0 EndX=-7.5 EndY=-9e-16 EndZ=0
    g27: LineSegment StartX=-7.5 StartY=-9e-16 StartZ=0 EndX=-13.3297 EndY=4.73117 EndZ=0
    g28: LineSegment StartX=-10.7622 StartY=9.17831 StartZ=0 EndX=-3.75 EndY=6.49519 EndZ=0
    g29: LineSegment StartX=-3.75 StartY=6.49519 StartZ=0 EndX=-2.56755 EndY=13.9095 EndZ=0
    g30: LineSegment StartX=2.56755 StartY=13.9095 StartZ=0 EndX=3.75 EndY=6.49519 EndZ=0
    g31: LineSegment StartX=3.75 StartY=6.49519 StartZ=0 EndX=10.7622 EndY=9.17831 EndZ=0
    g32: LineSegment [constr] StartX=11.6913 StartY=6.75 StartZ=0 EndX=-11.6913 EndY=-6.75 EndZ=0
  constraints (70):
    c: Coincident(g0,g1)
    c: Coincident(g1,g2)
    c: Coincident(g2,g3)
    c: Coincident(g3,g4)
    c: Coincident(g4,g5)
    c: Coincident(g5,g0)
    c: Equal(g0, g1-g5) x5
    c: PointOnObject(g0,g6)
    c: PointOnObject(g1,g6)
    c: PointOnObject(g2,g6)
    c: PointOnObject(g3,g6)
    c: PointOnObject(g4,g6)
    c: PointOnObject(g5,g6)
    c: Coincident(g6,g-1)
    c: Radius(g6) = 13.5
    c: Coincident(g7,g8)
    c: Coincident(g8,g9)
    c: Coincident(g9,g10)
    c: Coincident(g10,g11)
    c: Coincident(g11,g12)
    c: Coincident(g12,g7)
    c: Equal(g7, g8-g12) x5
    c: PointOnObject(g7,g13)
    c: PointOnObject(g8,g13)
    c: PointOnObject(g9,g13)
    c: PointOnObject(g10,g13)
    c: PointOnObject(g11,g13)
    c: PointOnObject(g12,g13)
    c: Coincident(g13,g-1)
    c: Radius(g13) = 7.5
    c: Coincident(g14,g4)
    c: Coincident(g15,g3)
    c: Coincident(g16,g2)
    c: Coincident(g17,g1)
    c: Coincident(g18,g0)
    c: Coincident(g19,g0)
    c: Coincident(g20,g7)
    c: Coincident(g21,g20)
    c: Coincident(g22,g11)
    c: Coincident(g23,g22)
    c: Coincident(g24,g10)
    c: Coincident(g25,g24)
    c: Coincident(g26,g9)
    c: Coincident(g28,g8)
    c: Coincident(g29,g28)
    c: Coincident(g30,g7)
    c: Coincident(g31,g30)
    c: Tangent(g22,g14) = 1.5708
    c: Tangent(g23,g15) = 1.5708
    c: Tangent(g24,g15) = 1.5708
    c: Tangent(g26,g16) = 1.5708
    c: Tangent(g21,g14) = 1.5708
    c: Tangent(g16,g25) = 1.5708
    c: Tangent(g29,g18) = 1.5708
    c: Tangent(g30,g18) = 1.5708
    c: Tangent(g31,g19) = 1.5708
    c: Tangent(g20,g19) = 1.5708
    c: Tangent(g27,g17) = 1.5708
    c: Tangent(g17,g28) = 1.5708
    c: Coincident(g27,g26)
    c: Equal(g14,g15)
    c: Equal(g15,g16)
    c: Equal(g16,g17)
    c: Equal(g17,g18)
    c: Equal(g18,g19)
    c: Radius(g14) = 2.6
    c: Coincident(g32,g19)
    c: Coincident(g32,g16)
    c: Perpendicular(g32,g7)
    c: PointOnObject(g18,g-2)
FEATURE [PartDesign::Pocket] Pocket465  label="Screwheads Montage005"
  BaseFeature = -> Fillet188
  Length = 3
  Length2 = 100
  Profile = -> Sketch1134
  Type = 0
FEATURE [Sketcher::SketchObject] Sketch1123
  MapMode = 5
  Placement = pos=(0,0,2) rot=(0,0,1;0rad)
  Support = -> [Pocket465]
  sketch-geometry (3):
    g0: Circle [constr] CenterX=0 CenterY=15 CenterZ=0 NormalX=0 NormalY=0 NormalZ=1 AngleXU=0 Radius=35
    g1: Circle CenterX=28.7228 CenterY=35 CenterZ=0 NormalX=0 NormalY=0 NormalZ=1 AngleXU=0 Radius=1.6
    g2: Circle CenterX=33.541 CenterY=25 CenterZ=0 NormalX=0 NormalY=0 NormalZ=1 AngleXU=0 Radius=1.6
  constraints (9):
    c: Radius(g0) = 35
    c: PointOnObject(g1,g0)
    c: PointOnObject(g2,g0)
    c: Equal(g2,g1)
    c: Radius(g2) = 1.6
    c: DistanceY(g2,g1) = 10
    c: DistanceY(g-1,g0) = 15
    c: DistanceY(g0,g2) = 10
    c: DistanceX(g-1,g0) = 0
FEATURE [PartDesign::Pocket] Pocket468  label="Screwholes Montage005"
  BaseFeature = -> Pocket465
  Length = 3
  Length2 = 100
  Profile = -> Sketch1123
  Type = 0
FEATURE [PartDesign::Pocket] Pocket463  label="Servohorn011"
  BaseFeature = -> Pocket468
  Length = 2
  Length2 = 100
  Profile = -> Sketch1124
  Type = 0
FEATURE [PartDesign::Chamfer] Chamfer284  label="M3 Nut Smooth Hole121"
  Base = -> Groove103 [Edge24,Edge23]
  BaseFeature = -> Groove103
  Size = 0.2
FEATURE [PartDesign::Body] Body299  label="M2 Nut040"
  Group = -> [Sketch1151,Pad494,Sketch1135,Groove103,Chamfer284,Sketch1133,Sketch1141]
  Origin = -> Origin527
  Placement = pos=(0,0,2.75) rot=(0,0,1;0rad)
  Tip = -> Chamfer284
FEATURE [PartDesign::Chamfer] Chamfer285  label="M3x8 Smooth072"
  Base = -> Pocket470 [Face11,Edge2,Edge24,Edge3]
  BaseFeature = -> Pocket470
  Size = 0.2
FEATURE [PartDesign::Body] Body315  label="M2x052"
  Group = -> [Sketch1132,Pad521,Sketch1129,Pad506,Sketch1140,Pocket470,Chamfer285]
  Origin = -> Origin566
  Tip = -> Chamfer285
FEATURE [PartDesign::Chamfer] Chamfer286  label="M3x8 Smooth073"
  Base = -> Pocket546 [Face11,Edge2,Edge24,Edge3]
  BaseFeature = -> Pocket546
  Size = 0.2
FEATURE [PartDesign::Body] Body375  label="M3x078"
  Group = -> [Sketch1183,Pad616,Sketch1197,Pad625,Sketch1264,Pocket546,Chamfer286]
  Origin = -> Origin448
  Placement = pos=(-14.15,14.15,-6) rot=(0,0,1;0rad)
  Tip = -> Chamfer286
FEATURE [PartDesign::Chamfer] Chamfer289  label="M3x8 Smooth074"
  Base = -> Pocket490 [Face11,Edge2,Edge24,Edge3]
  BaseFeature = -> Pocket490
  Size = 0.2
FEATURE [PartDesign::Body] Body328  label="M2x053"
  Group = -> [Sketch1368,Pad516,Sketch1272,Pad533,Sketch1289,Pocket490,Chamfer289]
  Origin = -> Origin441
  Placement = pos=(-115.144,-143.75,71.585) rot=(1,0,0;1.5708rad)
  Tip = -> Chamfer289
FEATURE [PartDesign::Chamfer] Chamfer290  label="M3 Nut Smooth Hole124"
  Base = -> Groove129 [Edge24,Edge23]
  BaseFeature = -> Groove129
  Size = 0.2
FEATURE [PartDesign::Body] Body363  label="M3 Nut065"
  Group = -> [Sketch1267,Pad629,Sketch1193,Groove129,Chamfer290]
  Origin = -> Origin550
  Placement = pos=(14.15,14.15,3.5) rot=(0,0,-1;0.261799rad)
  Tip = -> Chamfer290
FEATURE [PartDesign::Chamfer] Chamfer292  label="M3 Nut Smooth Hole125"
  Base = -> Groove102 [Edge24,Edge23]
  BaseFeature = -> Groove102
  Size = 0.2
FEATURE [PartDesign::Body] Body318  label="M2 Nut045"
  Group = -> [Sketch1131,Pad514,Sketch1120,Groove102,Chamfer292,Sketch1116,Sketch1118]
  Origin = -> Origin535
  Placement = pos=(0,0,2.75) rot=(0,0,1;0rad)
  Tip = -> Chamfer292
FEATURE [App::Part] Part136  label="M040"
  Group = -> [Body315,Body318]
  Origin = -> Origin519
  Placement = pos=(-9.8e-15,10.5,80) rot=(0,1,0;3.14159rad)
FEATURE [PartDesign::Chamfer] Chamfer293  label="M3x20 Smooth053"
  Base = -> Pocket534 [Face11,Edge2,Edge24,Edge3]
  BaseFeature = -> Pocket534
  Size = 0.2
FEATURE [PartDesign::Body] Body327  label="M3x067"
  Group = -> [Sketch1400,Pad573,Sketch1419,Pad579,Sketch1423,Pocket534,Chamfer293]
  Origin = -> Origin492
  Placement = pos=(-71.5,-25.55,62.05) rot=(-1,0,0;1.5708rad)
  Tip = -> Chamfer293
FEATURE [PartDesign::Chamfer] Chamfer295  label="M3x8 Smooth076"
  Base = -> Pocket475 [Face11,Edge2,Edge24,Edge3]
  BaseFeature = -> Pocket475
  Size = 0.2
FEATURE [PartDesign::Body] Body305  label="M2x050"
  Group = -> [Sketch1149,Pad513,Sketch1157,Pad507,Sketch1153,Pocket475,Chamfer295]
  Origin = -> Origin546
  Tip = -> Chamfer295
FEATURE [App::Part] Part140  label="M042"
  Group = -> [Body305,Body299]
  Origin = -> Origin539
  Placement = pos=(-9.1,-5.25,80) rot=(0,1,0;3.14159rad)
FEATURE [App::Part] Part138  label="Screws009"
  Group = -> [Part136,Part141,Part140,Part142,Part134,Part127]
  Origin = -> Origin544
  Placement = pos=(0,1.16e-14,23.75) rot=(1,0,0;3.14159rad)
FEATURE [PartDesign::Fillet] Fillet191  label="Ball Bearing Pocket Bottom Fillet002"
  Base = -> Pocket464 [Edge43]
  BaseFeature = -> Pocket464
  Radius = 1.8
FEATURE [PartDesign::Fillet] Fillet186  label="Smooth End Edge002"
  Base = -> Fillet191 [Edge31]
  BaseFeature = -> Fillet191
  Radius = 0.4
FEATURE [PartDesign::Body] Body349  label="Limb_Ball_Bearing_Mount_long_v006"
  Group = -> [Sketch1306,Pad510,Sketch1312,SubtractivePipe015,Fillet178,Sketch1172,Pocket496,Sketch1295,Pocket495,Sketch1300,Pocket474,Sketch1303,Pocket464,Fillet191,Fillet186]
  Origin = -> Origin432
  Tip = -> Fillet186
FEATURE [PartDesign::Chamfer] Chamfer296
  Base = -> Pocket559 [Edge3]
  BaseFeature = -> Pocket559
  Size = 0.25
FEATURE [PartDesign::Body] Body386  label="Gear011"
  Group = -> [Sketch1221,Pad648,Sketch1194,Pocket559,Chamfer296]
  Origin = -> Origin561
  Placement = pos=(0,0,38.25) rot=(0,0,1;0rad)
  Tip = -> Chamfer296
FEATURE [PartDesign::Fillet] Fillet192  label="Smooth Servhohorn Edges003"
  Base = -> Pocket463 [Edge124,Edge122,Edge129,Edge121,Edge136,Edge120]
  BaseFeature = -> Pocket463
  Radius = 1
FEATURE [Sketcher::SketchObject] Sketch1126
  MapMode = 5
  Placement = pos=(0,0,3) rot=(0,0,1;0rad)
  Support = -> [Fillet192]
  sketch-geometry (14):
    g0: LineSegment [constr] StartX=0 StartY=10.5 StartZ=0 EndX=-9.09327 EndY=5.25 EndZ=0
    g1: LineSegment [constr] StartX=-9.09327 StartY=5.25 StartZ=0 EndX=-9.09327 EndY=-5.25 EndZ=0
    g2: LineSegment [constr] StartX=-9.09327 StartY=-5.25 StartZ=0 EndX=0 EndY=-10.5 EndZ=0
    g3: LineSegment [constr] StartX=0 StartY=-10.5 StartZ=0 EndX=9.09327 EndY=-5.25 EndZ=0
    g4: LineSegment [constr] StartX=9.09327 StartY=-5.25 StartZ=0 EndX=9.09327 EndY=5.25 EndZ=0
    g5: LineSegment [constr] StartX=9.09327 StartY=5.25 StartZ=0 EndX=0 EndY=10.5 EndZ=0
    g6: Circle [constr] CenterX=0 CenterY=0 CenterZ=0 NormalX=0 NormalY=0 NormalZ=1 AngleXU=0 Radius=10.5
    g7: LineSegment [constr] StartX=0 StartY=10.5 StartZ=0 EndX=0 EndY=-10.5 EndZ=0
    g8: Circle CenterX=0 CenterY=10.5 CenterZ=0 NormalX=0 NormalY=0 NormalZ=1 AngleXU=0 Radius=0.95
    g9: Circle CenterX=9.09327 CenterY=5.25 CenterZ=0 NormalX=0 NormalY=0 NormalZ=1 AngleXU=0 Radius=0.95
    g10: Circle CenterX=9.09327 CenterY=-5.25 CenterZ=0 NormalX=0 NormalY=0 NormalZ=1 AngleXU=0 Radius=0.95
    g11: Circle CenterX=0 CenterY=-10.5 CenterZ=0 NormalX=0 NormalY=0 NormalZ=1 AngleXU=0 Radius=0.95
    g12: Circle CenterX=-9.09327 CenterY=-5.25 CenterZ=0 NormalX=0 NormalY=0 NormalZ=1 AngleXU=0 Radius=0.95
    g13: Circle CenterX=-9.09327 CenterY=5.25 CenterZ=0 NormalX=0 NormalY=0 NormalZ=1 AngleXU=0 Radius=0.95
  constraints (30):
    c: Coincident(g0,g1)
    c: Coincident(g1,g2)
    c: Coincident(g2,g3)
    c: Coincident(g3,g4)
    c: Coincident(g4,g5)
    c: Coincident(g5,g0)
    c: Equal(g0, g1-g5) x5
    c: PointOnObject(g0,g6)
    c: PointOnObject(g1,g6)
    c: PointOnObject(g2,g6)
    c: PointOnObject(g3,g6)
    c: PointOnObject(g4,g6)
    c: PointOnObject(g5,g6)
    c: Coincident(g6,g-1)
    c: Coincident(g7,g0)
    c: Coincident(g7,g2)
    c: Radius(g6) = 10.5
    c: Coincident(g8,g0)
    c: Coincident(g9,g4)
    c: Coincident(g10,g3)
    c: Coincident(g11,g2)
    c: Coincident(g12,g1)
    c: Coincident(g13,g0)
    c: Equal(g13,g12)
    c: Equal(g12,g11)
    c: Equal(g11,g10)
    c: Equal(g10,g9)
    c: Equal(g9,g8)
    c: Radius(g8) = 0.95
    c: PointOnObject(g8,g-2)
FEATURE [PartDesign::Pocket] Pocket462  label="Servohorn Mounting Holes003"
  BaseFeature = -> Fillet192
  Length = 3
  Length2 = 100
  Profile = -> Sketch1126
  Type = 0
FEATURE [Sketcher::SketchObject] Sketch1125
  MapMode = 5
  Placement = pos=(0,0,3) rot=(0,0,1;0rad)
  Support = -> [Pocket462]
  sketch-geometry (1):
    g0: Circle CenterX=0 CenterY=0 CenterZ=0 NormalX=0 NormalY=0 NormalZ=1 AngleXU=0 Radius=6.15
  constraints (2):
    c: Coincident(g0,g-1)
    c: Radius(g0) = 6.15
FEATURE [PartDesign::Pocket] Pocket457  label="Servohorn Axis003"
  BaseFeature = -> Pocket462
  Length = 3
  Length2 = 100
  Profile = -> Sketch1125
  Type = 0
FEATURE [PartDesign::Fillet] Fillet189  label="Smooth End Egde003"
  Base = -> Pocket457 [Edge150]
  BaseFeature = -> Pocket457
  Radius = 0.4
FEATURE [PartDesign::Body] Body311  label="Limb_Servohorn_Mount_long_v007"
  Group = -> [Sketch1130,Pad504,Sketch1115,SubtractivePipe011,Fillet188,Sketch1134,Pocket465,Sketch1123,Pocket468,Sketch1124,Pocket463,Fillet192,Sketch1126,Pocket462,Sketch1125,Pocket457,Fillet189]
  Origin = -> Origin515
  Tip = -> Fillet189
FEATURE [PartDesign::Chamfer] Chamfer299  label="M3 Nut Smooth Hole126"
  Base = -> Groove132 [Edge24,Edge23]
  BaseFeature = -> Groove132
  Size = 0.2
FEATURE [PartDesign::Body] Body364  label="M3 Nut066"
  Group = -> [Sketch1219,Pad566,Sketch1203,Groove132,Chamfer299]
  Origin = -> Origin417
  Placement = pos=(5e-14,-65.6,224.85) rot=(0.57735,-0.57735,0.57735;4.18879rad)
  Tip = -> Chamfer299
FEATURE [PartDesign::Chamfer] Chamfer300  label="M3x8 Smooth078"
  Base = -> Pocket527 [Face11,Edge2,Edge24,Edge3]
  BaseFeature = -> Pocket527
  Size = 0.2
FEATURE [PartDesign::Body] Body376  label="M3x079"
  Group = -> [Sketch1262,Pad614,Sketch1175,Pad605,Sketch1191,Pocket527,Chamfer300]
  Origin = -> Origin449
  Placement = pos=(14.15,-14.15,-6) rot=(0,0,1;0rad)
  Tip = -> Chamfer300
FEATURE [PartDesign::Chamfer] Chamfer301  label="M3 Nut Smooth Hole127"
  Base = -> Groove114 [Edge24,Edge23]
  BaseFeature = -> Groove114
  Size = 0.2
FEATURE [PartDesign::Body] Body381  label="M3 Nut070"
  Group = -> [Sketch1214,Pad555,Sketch1217,Groove114,Chamfer301]
  Origin = -> Origin510
  Placement = pos=(3.9e-14,-65.6,176.35) rot=(0.57735,-0.57735,0.57735;4.18879rad)
  Tip = -> Chamfer301
FEATURE [PartDesign::Chamfer] Chamfer302  label="M3x20 Smooth055"
  Base = -> Pocket522 [Face11,Edge2,Edge24,Edge3]
  BaseFeature = -> Pocket522
  Size = 0.2
FEATURE [PartDesign::Body] Body389  label="M3x084"
  Group = -> [Sketch1417,Pad595,Sketch1397,Pad600,Sketch1412,Pocket522,Chamfer302]
  Origin = -> Origin569
  Placement = pos=(-23,-25.6,62.05) rot=(-1,0,0;1.5708rad)
  Tip = -> Chamfer302
FEATURE [App::Part] Part135  label="Servo Screws002"
  Group = -> [Body327,Body348,Body389,Body334]
  Origin = -> Origin456
  Placement = pos=(0,1.4e-14,114.1) rot=(1,0,0;3.14159rad)
FEATURE [Part::Mirroring] Part__Mirroring004  label="Limb_Ball_Bearing_Mount_long_v005 (Mirror #5)"
  Base = (0,0,0)
  Normal = (0,0,1)
  Placement = pos=(0,0,-47.15) rot=(0,0,1;0rad)
  Source = -> Body349
FEATURE [App::Part] Part137  label="ball bearing moung002"
  Group = -> [Body349,Part__Mirroring004]
  Origin = -> Origin425
  Placement = pos=(-144.1,22.7,27.05) rot=(0,0.707107,0.707107;3.14159rad)
FEATURE [Part::Mirroring] Part__Mirroring007  label="Wrist001 (Mirror #2)"
  Base = (0,0,0)
  Normal = (0,0,1)
  Placement = pos=(0,0,0) rot=(1,0,0;3.14159rad)
  Source = -> Body351
FEATURE [App::Part] Part156  label="Lower Leg and foot002"
  Group = -> [Body351,Body326,Part__Mirroring007]
  Origin = -> Origin422
FEATURE [Part::Mirroring] Part__Mirroring005  label="Limb_Top_Shell001 (Mirror #6)"
  Base = (0,0,0)
  Normal = (0,0,1)
  Placement = pos=(0,-1.95,0) rot=(1,0,0;3.14159rad)
  Source = -> Body295
FEATURE [Part::Mirroring] Part__Mirroring002  label="Wrist_Counterpart001 (Mirror #3)"
  Base = (0,0,0)
  Normal = (0,0,1)
  Placement = pos=(0,-309.85,3.8e-14) rot=(1,0,0;3.14159rad)
  Source = -> Body296
FEATURE [Part::Mirroring] Part__Mirroring003  label="Limb_Servohorn_Mount_long_v006 (Mirror #4)"
  Base = (0,0,0)
  Normal = (0,0,1)
  Placement = pos=(0,0,-47.1) rot=(0,0,1;0rad)
  Source = -> Body311
FEATURE [App::Part] Part153  label="servohorn moun tpost002"
  Group = -> [Body311,Part143,Part138,Part__Mirroring003]
  Origin = -> Origin565
  Placement = pos=(-144.1,-24.45,27.05) rot=(1,0,0;1.5708rad)
FEATURE [Sketcher::SketchObject] Sketch1468
  MapMode = 5
  Placement = pos=(0,0,0) rot=(1,0,0;1.5708rad)
  Support = -> [XZ_Plane467]
  sketch-geometry (8):
    g0: LineSegment StartX=-1.5 StartY=2.25 StartZ=0 EndX=-3.25 EndY=2.25 EndZ=0
    g1: LineSegment StartX=-3.25 StartY=2.25 StartZ=0 EndX=-3.25 EndY=1.25 EndZ=0
    g2: LineSegment StartX=-3.25 StartY=1.25 StartZ=0 EndX=-2 EndY=1.25 EndZ=0
    g3: LineSegment StartX=-2 StartY=1.25 StartZ=0 EndX=-2 EndY=-1.25 EndZ=0
    g4: LineSegment StartX=-2 StartY=-1.25 StartZ=0 EndX=-3.25 EndY=-1.25 EndZ=0
    g5: LineSegment StartX=-3.25 StartY=-1.25 StartZ=0 EndX=-3.25 EndY=-2.25 EndZ=0
    g6: LineSegment StartX=-3.25 StartY=-2.25 StartZ=0 EndX=-1.5 EndY=-2.25 EndZ=0
    g7: LineSegment StartX=-1.5 StartY=-2.25 StartZ=0 EndX=-1.5 EndY=2.25 EndZ=0
  constraints (23):
    c: Horizontal(g0)
    c: Coincident(g0,g1)
    c: Vertical(g1)
    c: Coincident(g1,g2)
    c: Horizontal(g2)
    c: Coincident(g2,g3)
    c: Vertical(g3)
    c: Coincident(g3,g4)
    c: Horizontal(g4)
    c: Coincident(g4,g5)
    c: Vertical(g5)
    c: Coincident(g5,g6)
    c: Horizontal(g6)
    c: Coincident(g6,g7)
    c: Vertical(g7)
    c: Coincident(g0,g7)
    c: Equal(g1,g5)
    c: Symmetric(g4,g1,g-1)
    c: DistanceX(g0,g-1) = 1.5
    c: DistanceY(g3,g3) = 2.5
    c: DistanceY(g7,g7) = 4.5
    c: DistanceX(g0,g-1) = 3.25
    c: DistanceX(g2,g-1) = 2
FEATURE [PartDesign::Revolution] Revolution028
  Angle = 360
  Axis = (0,2e-16,1)
  Base = (0,0,0)
  Placement = pos=(0,0,0) rot=(1,0,0;1.5708rad)
  Profile = -> Sketch1468
  ReferenceAxis = -> Sketch1468 [V_Axis]
FEATURE [PartDesign::Fillet] Fillet148
  Base = -> Revolution028 [Face2,Face6,Edge1,Edge11,Face4]
  BaseFeature = -> Revolution028
  Placement = pos=(0,0,0) rot=(1,0,0;1.5708rad)
  Radius = 0.25
FEATURE [PartDesign::Body] Body361  label="Rubber Dampener026"
  Group = -> [Sketch1468,Revolution028,Fillet148]
  Origin = -> Origin500
  Placement = pos=(-55.25,-12.25,100.75) rot=(-1,0,0;1.5708rad)
  Tip = -> Fillet148
FEATURE [Sketcher::SketchObject] Sketch1469
  MapMode = 5
  Support = -> [XY_Plane421]
  sketch-geometry (8):
    g0: LineSegment StartX=0 StartY=2.3094 StartZ=0 EndX=-2 EndY=1.1547 EndZ=0
    g1: LineSegment StartX=-2 StartY=1.1547 StartZ=0 EndX=-2 EndY=-1.1547 EndZ=0
    g2: LineSegment StartX=-2 StartY=-1.1547 StartZ=0 EndX=-2e-16 EndY=-2.3094 EndZ=0
    g3: LineSegment StartX=-2e-16 StartY=-2.3094 StartZ=0 EndX=2 EndY=-1.1547 EndZ=0
    g4: LineSegment StartX=2 StartY=-1.1547 StartZ=0 EndX=2 EndY=1.1547 EndZ=0
    g5: LineSegment StartX=2 StartY=1.1547 StartZ=0 EndX=0 EndY=2.3094 EndZ=0
    g6: Circle [constr] CenterX=0 CenterY=0 CenterZ=0 NormalX=0 NormalY=0 NormalZ=1 AngleXU=0 Radius=2.3094
    g7: Circle CenterX=0 CenterY=0 CenterZ=0 NormalX=0 NormalY=0 NormalZ=1 AngleXU=0 Radius=1
  constraints (18):
    c: Coincident(g0,g1)
    c: Coincident(g1,g2)
    c: Coincident(g2,g3)
    c: Coincident(g3,g4)
    c: Coincident(g4,g5)
    c: Coincident(g5,g0)
    c: Equal(g0, g1-g5) x5
    c: PointOnObject(g0,g6)
    c: PointOnObject(g1,g6)
    c: PointOnObject(g2,g6)
    c: PointOnObject(g3,g6)
    c: PointOnObject(g4,g6)
    c: PointOnObject(g5,g6)
    c: Coincident(g6,g-1)
    c: PointOnObject(g5,g-2)
    c: DistanceX(g0,g4) = 4
    c: Coincident(g7,g-1)
    c: Radius(g7) = 1
FEATURE [PartDesign::Pad] Pad609  label="M3 Nut Primitive115"
  Length = 0.6
  Length2 = 0.6
  Profile = -> Sketch1469
  Type = 4
FEATURE [Sketcher::SketchObject] Sketch1427
  ExternalGeometry = -> [Pad609]
  MapMode = 5
  Placement = pos=(0,0,0) rot=(0.57735,0.57735,0.57735;2.0944rad)
  Support = -> [YZ_Plane412]
  sketch-geometry (6):
    g0: LineSegment StartX=-1.9594 StartY=0.6 StartZ=0 EndX=-2.8094 EndY=0.6 EndZ=0
    g1: LineSegment StartX=-2.8094 StartY=0.6 StartZ=0 EndX=-2.8094 EndY=-0.6 EndZ=0
    g2: LineSegment StartX=-2.8094 StartY=-0.6 StartZ=0 EndX=-1.9594 EndY=-0.6 EndZ=0
    g3: LineSegment StartX=-1.9594 StartY=-0.6 StartZ=0 EndX=-2.3094 EndY=-0.4 EndZ=0
    g4: LineSegment StartX=-2.3094 StartY=-0.4 StartZ=0 EndX=-2.3094 EndY=0.4 EndZ=0
    g5: LineSegment StartX=-2.3094 StartY=0.4 StartZ=0 EndX=-1.9594 EndY=0.6 EndZ=0
  constraints (15):
    c: Horizontal(g0)
    c: Coincident(g0,g1)
    c: Coincident(g1,g2)
    c: Coincident(g2,g3)
    c: Coincident(g3,g4)
    c: Coincident(g4,g5)
    c: Coincident(g5,g0)
    c: Symmetric(g4,g3,g-1)
    c: Symmetric(g0,g2,g-1)
    c: Symmetric(g1,g0,g-1)
    c: DistanceX(g0,g4) = 0.5
    c: DistanceY(g3,g4) = 0.8
    c: DistanceY(g1,g0) = 1.2
    c: PointOnObject(g3,g-3)
    c: DistanceX(g4,g0) = 0.35
FEATURE [PartDesign::Groove] Groove120  label="M3 Nut Smooth114"
  Angle = 360
  Axis = (-2e-16,3e-16,1)
  Base = (0,0,0)
  BaseFeature = -> Pad609
  Profile = -> Sketch1427
  ReferenceAxis = -> Sketch1427 [V_Axis]
  Reversed = true
FEATURE [PartDesign::Chamfer] Chamfer259  label="M3 Nut Smooth Hole110"
  Base = -> Groove120 [Edge24,Edge23]
  BaseFeature = -> Groove120
  Size = 0.2
FEATURE [PartDesign::Body] Body352  label="M2 Nut048"
  Group = -> [Sketch1469,Pad609,Sketch1427,Groove120,Chamfer259,Sketch1429,Sketch1232]
  Origin = -> Origin554
  Placement = pos=(0,0,2.75) rot=(0,0,1;0rad)
  Tip = -> Chamfer259
FEATURE [Sketcher::SketchObject] Sketch1470
  MapMode = 5
  Placement = pos=(0,0,0) rot=(1,0,0;1.5708rad)
  Support = -> [XZ_Plane468]
  sketch-geometry (8):
    g0: LineSegment StartX=-1.5 StartY=2.25 StartZ=0 EndX=-3.25 EndY=2.25 EndZ=0
    g1: LineSegment StartX=-3.25 StartY=2.25 StartZ=0 EndX=-3.25 EndY=1.25 EndZ=0
    g2: LineSegment StartX=-3.25 StartY=1.25 StartZ=0 EndX=-2 EndY=1.25 EndZ=0
    g3: LineSegment StartX=-2 StartY=1.25 StartZ=0 EndX=-2 EndY=-1.25 EndZ=0
    g4: LineSegment StartX=-2 StartY=-1.25 StartZ=0 EndX=-3.25 EndY=-1.25 EndZ=0
    g5: LineSegment StartX=-3.25 StartY=-1.25 StartZ=0 EndX=-3.25 EndY=-2.25 EndZ=0
    g6: LineSegment StartX=-3.25 StartY=-2.25 StartZ=0 EndX=-1.5 EndY=-2.25 EndZ=0
    g7: LineSegment StartX=-1.5 StartY=-2.25 StartZ=0 EndX=-1.5 EndY=2.25 EndZ=0
  constraints (23):
    c: Horizontal(g0)
    c: Coincident(g0,g1)
    c: Vertical(g1)
    c: Coincident(g1,g2)
    c: Horizontal(g2)
    c: Coincident(g2,g3)
    c: Vertical(g3)
    c: Coincident(g3,g4)
    c: Horizontal(g4)
    c: Coincident(g4,g5)
    c: Vertical(g5)
    c: Coincident(g5,g6)
    c: Horizontal(g6)
    c: Coincident(g6,g7)
    c: Vertical(g7)
    c: Coincident(g0,g7)
    c: Equal(g1,g5)
    c: Symmetric(g4,g1,g-1)
    c: DistanceX(g0,g-1) = 1.5
    c: DistanceY(g3,g3) = 2.5
    c: DistanceY(g7,g7) = 4.5
    c: DistanceX(g0,g-1) = 3.25
    c: DistanceX(g2,g-1) = 2
FEATURE [PartDesign::Revolution] Revolution034
  Angle = 360
  Axis = (0,2e-16,1)
  Base = (0,0,0)
  Placement = pos=(0,0,0) rot=(1,0,0;1.5708rad)
  Profile = -> Sketch1470
  ReferenceAxis = -> Sketch1470 [V_Axis]
FEATURE [PartDesign::Fillet] Fillet171
  Base = -> Revolution034 [Face2,Face6,Edge1,Edge11,Face4]
  BaseFeature = -> Revolution034
  Placement = pos=(0,0,0) rot=(1,0,0;1.5708rad)
  Radius = 0.25
FEATURE [PartDesign::Body] Body393  label="Rubber Dampener032"
  Group = -> [Sketch1470,Revolution034,Fillet171]
  Origin = -> Origin481
  Placement = pos=(-62.3,-12.25,93.7) rot=(-1,0,0;1.5708rad)
  Tip = -> Fillet171
FEATURE [Sketcher::SketchObject] Sketch1471
  MapMode = 5
  Placement = pos=(0,0,0) rot=(1,0,0;1.5708rad)
  Support = -> [XZ_Plane457]
  sketch-geometry (8):
    g0: LineSegment StartX=-1.5 StartY=2.25 StartZ=0 EndX=-3.25 EndY=2.25 EndZ=0
    g1: LineSegment StartX=-3.25 StartY=2.25 StartZ=0 EndX=-3.25 EndY=1.25 EndZ=0
    g2: LineSegment StartX=-3.25 StartY=1.25 StartZ=0 EndX=-2 EndY=1.25 EndZ=0
    g3: LineSegment StartX=-2 StartY=1.25 StartZ=0 EndX=-2 EndY=-1.25 EndZ=0
    g4: LineSegment StartX=-2 StartY=-1.25 StartZ=0 EndX=-3.25 EndY=-1.25 EndZ=0
    g5: LineSegment StartX=-3.25 StartY=-1.25 StartZ=0 EndX=-3.25 EndY=-2.25 EndZ=0
    g6: LineSegment StartX=-3.25 StartY=-2.25 StartZ=0 EndX=-1.5 EndY=-2.25 EndZ=0
    g7: LineSegment StartX=-1.5 StartY=-2.25 StartZ=0 EndX=-1.5 EndY=2.25 EndZ=0
  constraints (23):
    c: Horizontal(g0)
    c: Coincident(g0,g1)
    c: Vertical(g1)
    c: Coincident(g1,g2)
    c: Horizontal(g2)
    c: Coincident(g2,g3)
    c: Vertical(g3)
    c: Coincident(g3,g4)
    c: Horizontal(g4)
    c: Coincident(g4,g5)
    c: Vertical(g5)
    c: Coincident(g5,g6)
    c: Horizontal(g6)
    c: Coincident(g6,g7)
    c: Vertical(g7)
    c: Coincident(g0,g7)
    c: Equal(g1,g5)
    c: Symmetric(g4,g1,g-1)
    c: DistanceX(g0,g-1) = 1.5
    c: DistanceY(g3,g3) = 2.5
    c: DistanceY(g7,g7) = 4.5
    c: DistanceX(g0,g-1) = 3.25
    c: DistanceX(g2,g-1) = 2
FEATURE [PartDesign::Revolution] Revolution032
  Angle = 360
  Axis = (0,2e-16,1)
  Base = (0,0,0)
  Placement = pos=(0,0,0) rot=(1,0,0;1.5708rad)
  Profile = -> Sketch1471
  ReferenceAxis = -> Sketch1471 [V_Axis]
FEATURE [PartDesign::Fillet] Fillet151
  Base = -> Revolution032 [Face2,Face6,Edge1,Edge11,Face4]
  BaseFeature = -> Revolution032
  Placement = pos=(0,0,0) rot=(1,0,0;1.5708rad)
  Radius = 0.25
FEATURE [PartDesign::Body] Body359  label="Rubber Dampener025"
  Group = -> [Sketch1471,Revolution032,Fillet151]
  Origin = -> Origin502
  Placement = pos=(-55.25,-12.25,100.75) rot=(-1,0,0;1.5708rad)
  Tip = -> Fillet151
FEATURE [Sketcher::SketchObject] Sketch1472
  MapMode = 5
  Support = -> [XY_Plane518]
  sketch-geometry (1):
    g0: Circle CenterX=0 CenterY=0 CenterZ=0 NormalX=0 NormalY=0 NormalZ=1 AngleXU=0 Radius=1.9
  constraints (2):
    c: Coincident(g0,g-1)
    c: Radius(g0) = 1.9
FEATURE [PartDesign::Pad] Pad623  label="M3x8 Head076"
  Length = 2
  Length2 = 100
  Profile = -> Sketch1472
  Type = 0
FEATURE [Sketcher::SketchObject] Sketch1473
  MapMode = 5
  Placement = pos=(0,0,0) rot=(1,0,0;1.5708rad)
  Support = -> [XZ_Plane466]
  sketch-geometry (8):
    g0: LineSegment StartX=-1.5 StartY=2.25 StartZ=0 EndX=-3.25 EndY=2.25 EndZ=0
    g1: LineSegment StartX=-3.25 StartY=2.25 StartZ=0 EndX=-3.25 EndY=1.25 EndZ=0
    g2: LineSegment StartX=-3.25 StartY=1.25 StartZ=0 EndX=-2 EndY=1.25 EndZ=0
    g3: LineSegment StartX=-2 StartY=1.25 StartZ=0 EndX=-2 EndY=-1.25 EndZ=0
    g4: LineSegment StartX=-2 StartY=-1.25 StartZ=0 EndX=-3.25 EndY=-1.25 EndZ=0
    g5: LineSegment StartX=-3.25 StartY=-1.25 StartZ=0 EndX=-3.25 EndY=-2.25 EndZ=0
    g6: LineSegment StartX=-3.25 StartY=-2.25 StartZ=0 EndX=-1.5 EndY=-2.25 EndZ=0
    g7: LineSegment StartX=-1.5 StartY=-2.25 StartZ=0 EndX=-1.5 EndY=2.25 EndZ=0
  constraints (23):
    c: Horizontal(g0)
    c: Coincident(g0,g1)
    c: Vertical(g1)
    c: Coincident(g1,g2)
    c: Horizontal(g2)
    c: Coincident(g2,g3)
    c: Vertical(g3)
    c: Coincident(g3,g4)
    c: Horizontal(g4)
    c: Coincident(g4,g5)
    c: Vertical(g5)
    c: Coincident(g5,g6)
    c: Horizontal(g6)
    c: Coincident(g6,g7)
    c: Vertical(g7)
    c: Coincident(g0,g7)
    c: Equal(g1,g5)
    c: Symmetric(g4,g1,g-1)
    c: DistanceX(g0,g-1) = 1.5
    c: DistanceY(g3,g3) = 2.5
    c: DistanceY(g7,g7) = 4.5
    c: DistanceX(g0,g-1) = 3.25
    c: DistanceX(g2,g-1) = 2
FEATURE [PartDesign::Revolution] Revolution025
  Angle = 360
  Axis = (0,2e-16,1)
  Base = (0,0,0)
  Placement = pos=(0,0,0) rot=(1,0,0;1.5708rad)
  Profile = -> Sketch1473
  ReferenceAxis = -> Sketch1473 [V_Axis]
FEATURE [PartDesign::Fillet] Fillet173
  Base = -> Revolution025 [Face2,Face6,Edge1,Edge11,Face4]
  BaseFeature = -> Revolution025
  Placement = pos=(0,0,0) rot=(1,0,0;1.5708rad)
  Radius = 0.25
FEATURE [PartDesign::Body] Body362  label="Rubber Dampener027"
  Group = -> [Sketch1473,Revolution025,Fillet173]
  Origin = -> Origin464
  Placement = pos=(-96.5,-12.25,127.7) rot=(-1,0,0;1.5708rad)
  Tip = -> Fillet173
FEATURE [App::Part] Part121  label="Rubber Dampeners008"
  Group = -> [Body394,Body362,Body356,Body390]
  Origin = -> Origin485
  Placement = pos=(87.2923,32.35,29.8753) rot=(0,1,0;5.49779rad)
FEATURE [Sketcher::SketchObject] Sketch1476
  MapMode = 5
  Placement = pos=(0,0,0) rot=(1,0,0;1.5708rad)
  Support = -> [XZ_Plane465]
  sketch-geometry (8):
    g0: LineSegment StartX=-1.5 StartY=2.25 StartZ=0 EndX=-3.25 EndY=2.25 EndZ=0
    g1: LineSegment StartX=-3.25 StartY=2.25 StartZ=0 EndX=-3.25 EndY=1.25 EndZ=0
    g2: LineSegment StartX=-3.25 StartY=1.25 StartZ=0 EndX=-2 EndY=1.25 EndZ=0
    g3: LineSegment StartX=-2 StartY=1.25 StartZ=0 EndX=-2 EndY=-1.25 EndZ=0
    g4: LineSegment StartX=-2 StartY=-1.25 StartZ=0 EndX=-3.25 EndY=-1.25 EndZ=0
    g5: LineSegment StartX=-3.25 StartY=-1.25 StartZ=0 EndX=-3.25 EndY=-2.25 EndZ=0
    g6: LineSegment StartX=-3.25 StartY=-2.25 StartZ=0 EndX=-1.5 EndY=-2.25 EndZ=0
    g7: LineSegment StartX=-1.5 StartY=-2.25 StartZ=0 EndX=-1.5 EndY=2.25 EndZ=0
  constraints (23):
    c: Horizontal(g0)
    c: Coincident(g0,g1)
    c: Vertical(g1)
    c: Coincident(g1,g2)
    c: Horizontal(g2)
    c: Coincident(g2,g3)
    c: Vertical(g3)
    c: Coincident(g3,g4)
    c: Horizontal(g4)
    c: Coincident(g4,g5)
    c: Vertical(g5)
    c: Coincident(g5,g6)
    c: Horizontal(g6)
    c: Coincident(g6,g7)
    c: Vertical(g7)
    c: Coincident(g0,g7)
    c: Equal(g1,g5)
    c: Symmetric(g4,g1,g-1)
    c: DistanceX(g0,g-1) = 1.5
    c: DistanceY(g3,g3) = 2.5
    c: DistanceY(g7,g7) = 4.5
    c: DistanceX(g0,g-1) = 3.25
    c: DistanceX(g2,g-1) = 2
FEATURE [PartDesign::Revolution] Revolution029
  Angle = 360
  Axis = (0,2e-16,1)
  Base = (0,0,0)
  Placement = pos=(0,0,0) rot=(1,0,0;1.5708rad)
  Profile = -> Sketch1476
  ReferenceAxis = -> Sketch1476 [V_Axis]
FEATURE [PartDesign::Fillet] Fillet190
  Base = -> Revolution029 [Face2,Face6,Edge1,Edge11,Face4]
  BaseFeature = -> Revolution029
  Placement = pos=(0,0,0) rot=(1,0,0;1.5708rad)
  Radius = 0.25
FEATURE [PartDesign::Body] Body392  label="Rubber Dampener031"
  Group = -> [Sketch1476,Revolution029,Fillet190]
  Origin = -> Origin458
  Placement = pos=(-89.5,-12.25,134.7) rot=(-1,0,0;1.5708rad)
  Tip = -> Fillet190
FEATURE [App::Part] Part118  label="Rubber Dampeners006"
  Group = -> [Body392,Body374,Body359,Body369]
  Origin = -> Origin454
  Placement = pos=(0,24.35,0) rot=(0,0,1;0rad)
FEATURE [Sketcher::SketchObject] Sketch1478
  MapMode = 5
  Placement = pos=(0,0,3) rot=(0,0,1;0rad)
  Support = -> [Pad568]
  sketch-geometry (1):
    g0: Circle CenterX=0 CenterY=0 CenterZ=0 NormalX=0 NormalY=0 NormalZ=1 AngleXU=0 Radius=1.5
  constraints (2):
    c: Coincident(g0,g-1)
    c: Radius(g0) = 1.5
FEATURE [PartDesign::Pad] Pad552  label="M3x20 Thread043"
  BaseFeature = -> Pad568
  Length = 20
  Length2 = 100
  Profile = -> Sketch1478
  Type = 0
FEATURE [Sketcher::SketchObject] Sketch1479
  MapMode = 5
  Placement = pos=(0,0,0) rot=(1,0,0;1.5708rad)
  Support = -> [XZ_Plane470]
  sketch-geometry (8):
    g0: LineSegment StartX=-1.5 StartY=2.25 StartZ=0 EndX=-3.25 EndY=2.25 EndZ=0
    g1: LineSegment StartX=-3.25 StartY=2.25 StartZ=0 EndX=-3.25 EndY=1.25 EndZ=0
    g2: LineSegment StartX=-3.25 StartY=1.25 StartZ=0 EndX=-2 EndY=1.25 EndZ=0
    g3: LineSegment StartX=-2 StartY=1.25 StartZ=0 EndX=-2 EndY=-1.25 EndZ=0
    g4: LineSegment StartX=-2 StartY=-1.25 StartZ=0 EndX=-3.25 EndY=-1.25 EndZ=0
    g5: LineSegment StartX=-3.25 StartY=-1.25 StartZ=0 EndX=-3.25 EndY=-2.25 EndZ=0
    g6: LineSegment StartX=-3.25 StartY=-2.25 StartZ=0 EndX=-1.5 EndY=-2.25 EndZ=0
    g7: LineSegment StartX=-1.5 StartY=-2.25 StartZ=0 EndX=-1.5 EndY=2.25 EndZ=0
  constraints (23):
    c: Horizontal(g0)
    c: Coincident(g0,g1)
    c: Vertical(g1)
    c: Coincident(g1,g2)
    c: Horizontal(g2)
    c: Coincident(g2,g3)
    c: Vertical(g3)
    c: Coincident(g3,g4)
    c: Horizontal(g4)
    c: Coincident(g4,g5)
    c: Vertical(g5)
    c: Coincident(g5,g6)
    c: Horizontal(g6)
    c: Coincident(g6,g7)
    c: Vertical(g7)
    c: Coincident(g0,g7)
    c: Equal(g1,g5)
    c: Symmetric(g4,g1,g-1)
    c: DistanceX(g0,g-1) = 1.5
    c: DistanceY(g3,g3) = 2.5
    c: DistanceY(g7,g7) = 4.5
    c: DistanceX(g0,g-1) = 3.25
    c: DistanceX(g2,g-1) = 2
FEATURE [PartDesign::Revolution] Revolution026
  Angle = 360
  Axis = (0,2e-16,1)
  Base = (0,0,0)
  Placement = pos=(0,0,0) rot=(1,0,0;1.5708rad)
  Profile = -> Sketch1479
  ReferenceAxis = -> Sketch1479 [V_Axis]
FEATURE [PartDesign::Fillet] Fillet163
  Base = -> Revolution026 [Face2,Face6,Edge1,Edge11,Face4]
  BaseFeature = -> Revolution026
  Placement = pos=(0,0,0) rot=(1,0,0;1.5708rad)
  Radius = 0.25
FEATURE [PartDesign::Body] Body396  label="Rubber Dampener035"
  Group = -> [Sketch1479,Revolution026,Fillet163]
  Origin = -> Origin468
  Placement = pos=(-96.5,-12.25,127.7) rot=(-1,0,0;1.5708rad)
  Tip = -> Fillet163
FEATURE [Sketcher::SketchObject] Sketch1480
  MapMode = 5
  Placement = pos=(0,0,0) rot=(1,0,0;1.5708rad)
  Support = -> [XZ_Plane464]
  sketch-geometry (8):
    g0: LineSegment StartX=-1.5 StartY=2.25 StartZ=0 EndX=-3.25 EndY=2.25 EndZ=0
    g1: LineSegment StartX=-3.25 StartY=2.25 StartZ=0 EndX=-3.25 EndY=1.25 EndZ=0
    g2: LineSegment StartX=-3.25 StartY=1.25 StartZ=0 EndX=-2 EndY=1.25 EndZ=0
    g3: LineSegment StartX=-2 StartY=1.25 StartZ=0 EndX=-2 EndY=-1.25 EndZ=0
    g4: LineSegment StartX=-2 StartY=-1.25 StartZ=0 EndX=-3.25 EndY=-1.25 EndZ=0
    g5: LineSegment StartX=-3.25 StartY=-1.25 StartZ=0 EndX=-3.25 EndY=-2.25 EndZ=0
    g6: LineSegment StartX=-3.25 StartY=-2.25 StartZ=0 EndX=-1.5 EndY=-2.25 EndZ=0
    g7: LineSegment StartX=-1.5 StartY=-2.25 StartZ=0 EndX=-1.5 EndY=2.25 EndZ=0
  constraints (23):
    c: Horizontal(g0)
    c: Coincident(g0,g1)
    c: Vertical(g1)
    c: Coincident(g1,g2)
    c: Horizontal(g2)
    c: Coincident(g2,g3)
    c: Vertical(g3)
    c: Coincident(g3,g4)
    c: Horizontal(g4)
    c: Coincident(g4,g5)
    c: Vertical(g5)
    c: Coincident(g5,g6)
    c: Horizontal(g6)
    c: Coincident(g6,g7)
    c: Vertical(g7)
    c: Coincident(g0,g7)
    c: Equal(g1,g5)
    c: Symmetric(g4,g1,g-1)
    c: DistanceX(g0,g-1) = 1.5
    c: DistanceY(g3,g3) = 2.5
    c: DistanceY(g7,g7) = 4.5
    c: DistanceX(g0,g-1) = 3.25
    c: DistanceX(g2,g-1) = 2
FEATURE [PartDesign::Revolution] Revolution031
  Angle = 360
  Axis = (0,2e-16,1)
  Base = (0,0,0)
  Placement = pos=(0,0,0) rot=(1,0,0;1.5708rad)
  Profile = -> Sketch1480
  ReferenceAxis = -> Sketch1480 [V_Axis]
FEATURE [PartDesign::Fillet] Fillet161
  Base = -> Revolution031 [Face2,Face6,Edge1,Edge11,Face4]
  BaseFeature = -> Revolution031
  Placement = pos=(0,0,0) rot=(1,0,0;1.5708rad)
  Radius = 0.25
FEATURE [PartDesign::Body] Body395  label="Rubber Dampener034"
  Group = -> [Sketch1480,Revolution031,Fillet161]
  Origin = -> Origin487
  Placement = pos=(-89.5,-12.25,134.7) rot=(-1,0,0;1.5708rad)
  Tip = -> Fillet161
FEATURE [App::Part] Part120  label="Rubber Dampeners007"
  Group = -> [Body395,Body396,Body361,Body393]
  Origin = -> Origin453
  Placement = pos=(18.7923,-33.3866,66.0791) rot=(0.357407,0.357407,-0.862856;1.71777rad)
FEATURE [Sketcher::SketchObject] Sketch1481
  MapMode = 5
  Placement = pos=(0,0,2) rot=(0,0,1;0rad)
  Support = -> [Pad623]
  sketch-geometry (1):
    g0: Circle CenterX=0 CenterY=0 CenterZ=0 NormalX=0 NormalY=0 NormalZ=1 AngleXU=0 Radius=1
  constraints (2):
    c: Coincident(g0,g-1)
    c: Radius(g0) = 1
FEATURE [PartDesign::Pad] Pad617  label="M3x8 Thread071"
  BaseFeature = -> Pad623
  Length = 8
  Length2 = 100
  Profile = -> Sketch1481
  Type = 0
FEATURE [Sketcher::SketchObject] Sketch1483
  MapMode = 5
  Support = -> [XY_Plane511]
  sketch-geometry (1):
    g0: Circle CenterX=0 CenterY=0 CenterZ=0 NormalX=0 NormalY=0 NormalZ=1 AngleXU=0 Radius=1.9
  constraints (2):
    c: Coincident(g0,g-1)
    c: Radius(g0) = 1.9
FEATURE [PartDesign::Pad] Pad602  label="M3x8 Head067"
  Length = 2
  Length2 = 100
  Profile = -> Sketch1483
  Type = 0
FEATURE [Sketcher::SketchObject] Sketch1484
  MapMode = 5
  Placement = pos=(0,0,2) rot=(0,0,1;0rad)
  Support = -> [Pad618]
  sketch-geometry (1):
    g0: Circle CenterX=0 CenterY=0 CenterZ=0 NormalX=0 NormalY=0 NormalZ=1 AngleXU=0 Radius=1
  constraints (2):
    c: Coincident(g0,g-1)
    c: Radius(g0) = 1
FEATURE [PartDesign::Pad] Pad620  label="M3x8 Thread072"
  BaseFeature = -> Pad618
  Length = 8
  Length2 = 100
  Profile = -> Sketch1484
  Type = 0
FEATURE [Sketcher::SketchObject] Sketch1475
  MapMode = 5
  Placement = pos=(0,0,0) rot=(1,0,0;3.14159rad)
  Support = -> [Pad620]
  sketch-geometry (7):
    g0: LineSegment StartX=0.77 StartY=0.44456 StartZ=0 EndX=0 EndY=0.889119 EndZ=0
    g1: LineSegment StartX=0 StartY=0.889119 StartZ=0 EndX=-0.77 EndY=0.44456 EndZ=0
    g2: LineSegment StartX=-0.77 StartY=0.44456 StartZ=0 EndX=-0.77 EndY=-0.44456 EndZ=0
    g3: LineSegment StartX=-0.77 StartY=-0.44456 StartZ=0 EndX=3.85628e-11 EndY=-0.889119 EndZ=0
    g4: LineSegment StartX=3.85628e-11 StartY=-0.889119 StartZ=0 EndX=0.77 EndY=-0.44456 EndZ=0
    g5: LineSegment StartX=0.77 StartY=-0.44456 StartZ=0 EndX=0.77 EndY=0.44456 EndZ=0
    g6: Circle [constr] CenterX=0 CenterY=0 CenterZ=0 NormalX=0 NormalY=0 NormalZ=1 AngleXU=0 Radius=0.889119
  constraints (16):
    c: Coincident(g0,g1)
    c: Coincident(g1,g2)
    c: Coincident(g2,g3)
    c: Coincident(g3,g4)
    c: Coincident(g4,g5)
    c: Coincident(g5,g0)
    c: Equal(g0, g1-g5) x5
    c: PointOnObject(g0,g6)
    c: PointOnObject(g1,g6)
    c: PointOnObject(g2,g6)
    c: PointOnObject(g3,g6)
    c: PointOnObject(g4,g6)
    c: PointOnObject(g5,g6)
    c: Coincident(g6,g-1)
    c: PointOnObject(g0,g-2)
    c: DistanceX(g1,g0) = 1.54
FEATURE [PartDesign::Pocket] Pocket535  label="M3x8 Wrench069"
  BaseFeature = -> Pad620
  Length = 1
  Length2 = 100
  Profile = -> Sketch1475
  Type = 0
FEATURE [PartDesign::Chamfer] Chamfer261  label="M3x8 Smooth065"
  Base = -> Pocket535 [Face11,Edge2,Edge24,Edge3]
  BaseFeature = -> Pocket535
  Size = 0.2
FEATURE [PartDesign::Body] Body358  label="M2x055"
  Group = -> [Sketch1258,Pad618,Sketch1484,Pad620,Sketch1475,Pocket535,Chamfer261]
  Origin = -> Origin423
  Tip = -> Chamfer261
FEATURE [App::Part] Part147  label="M046"
  Group = -> [Body358,Body352]
  Origin = -> Origin490
  Placement = pos=(-9.8e-15,-10.5,80) rot=(0,1,0;3.14159rad)
FEATURE [Sketcher::SketchObject] Sketch1486
  MapMode = 5
  Support = -> [XY_Plane540]
  sketch-geometry (8):
    g0: LineSegment StartX=0 StartY=2.3094 StartZ=0 EndX=-2 EndY=1.1547 EndZ=0
    g1: LineSegment StartX=-2 StartY=1.1547 StartZ=0 EndX=-2 EndY=-1.1547 EndZ=0
    g2: LineSegment StartX=-2 StartY=-1.1547 StartZ=0 EndX=-2e-16 EndY=-2.3094 EndZ=0
    g3: LineSegment StartX=-2e-16 StartY=-2.3094 StartZ=0 EndX=2 EndY=-1.1547 EndZ=0
    g4: LineSegment StartX=2 StartY=-1.1547 StartZ=0 EndX=2 EndY=1.1547 EndZ=0
    g5: LineSegment StartX=2 StartY=1.1547 StartZ=0 EndX=0 EndY=2.3094 EndZ=0
    g6: Circle [constr] CenterX=0 CenterY=0 CenterZ=0 NormalX=0 NormalY=0 NormalZ=1 AngleXU=0 Radius=2.3094
    g7: Circle CenterX=0 CenterY=0 CenterZ=0 NormalX=0 NormalY=0 NormalZ=1 AngleXU=0 Radius=1
  constraints (18):
    c: Coincident(g0,g1)
    c: Coincident(g1,g2)
    c: Coincident(g2,g3)
    c: Coincident(g3,g4)
    c: Coincident(g4,g5)
    c: Coincident(g5,g0)
    c: Equal(g0, g1-g5) x5
    c: PointOnObject(g0,g6)
    c: PointOnObject(g1,g6)
    c: PointOnObject(g2,g6)
    c: PointOnObject(g3,g6)
    c: PointOnObject(g4,g6)
    c: PointOnObject(g5,g6)
    c: Coincident(g6,g-1)
    c: PointOnObject(g5,g-2)
    c: DistanceX(g0,g4) = 4
    c: Coincident(g7,g-1)
    c: Radius(g7) = 1
FEATURE [PartDesign::Pad] Pad633  label="M3 Nut Primitive119"
  Length = 0.6
  Length2 = 0.6
  Profile = -> Sketch1486
  Type = 4
FEATURE [Sketcher::SketchObject] Sketch1474
  ExternalGeometry = -> [Pad633]
  MapMode = 5
  Placement = pos=(0,0,0) rot=(0.57735,0.57735,0.57735;2.0944rad)
  Support = -> [YZ_Plane434]
  sketch-geometry (6):
    g0: LineSegment StartX=-1.9594 StartY=0.6 StartZ=0 EndX=-2.8094 EndY=0.6 EndZ=0
    g1: LineSegment StartX=-2.8094 StartY=0.6 StartZ=0 EndX=-2.8094 EndY=-0.6 EndZ=0
    g2: LineSegment StartX=-2.8094 StartY=-0.6 StartZ=0 EndX=-1.9594 EndY=-0.6 EndZ=0
    g3: LineSegment StartX=-1.9594 StartY=-0.6 StartZ=0 EndX=-2.3094 EndY=-0.4 EndZ=0
    g4: LineSegment StartX=-2.3094 StartY=-0.4 StartZ=0 EndX=-2.3094 EndY=0.4 EndZ=0
    g5: LineSegment StartX=-2.3094 StartY=0.4 StartZ=0 EndX=-1.9594 EndY=0.6 EndZ=0
  constraints (15):
    c: Horizontal(g0)
    c: Coincident(g0,g1)
    c: Coincident(g1,g2)
    c: Coincident(g2,g3)
    c: Coincident(g3,g4)
    c: Coincident(g4,g5)
    c: Coincident(g5,g0)
    c: Symmetric(g4,g3,g-1)
    c: Symmetric(g0,g2,g-1)
    c: Symmetric(g1,g0,g-1)
    c: DistanceX(g0,g4) = 0.5
    c: DistanceY(g3,g4) = 0.8
    c: DistanceY(g1,g0) = 1.2
    c: PointOnObject(g3,g-3)
    c: DistanceX(g4,g0) = 0.35
FEATURE [PartDesign::Groove] Groove125  label="M3 Nut Smooth119"
  Angle = 360
  Axis = (-2e-16,3e-16,1)
  Base = (0,0,0)
  BaseFeature = -> Pad633
  Profile = -> Sketch1474
  ReferenceAxis = -> Sketch1474 [V_Axis]
  Reversed = true
FEATURE [PartDesign::Chamfer] Chamfer287  label="M3 Nut Smooth Hole122"
  Base = -> Groove125 [Edge24,Edge23]
  BaseFeature = -> Groove125
  Size = 0.2
FEATURE [PartDesign::Body] Body357  label="M2 Nut049"
  Group = -> [Sketch1486,Pad633,Sketch1474,Groove125,Chamfer287,Sketch1257,Sketch1238]
  Origin = -> Origin508
  Placement = pos=(0,0,2.75) rot=(0,0,1;0rad)
  Tip = -> Chamfer287
FEATURE [Sketcher::SketchObject] Sketch1487
  MapMode = 5
  Placement = pos=(0,0,0) rot=(1,0,0;3.14159rad)
  Support = -> [Pad617]
  sketch-geometry (7):
    g0: LineSegment StartX=0.77 StartY=0.44456 StartZ=0 EndX=0 EndY=0.889119 EndZ=0
    g1: LineSegment StartX=0 StartY=0.889119 StartZ=0 EndX=-0.77 EndY=0.44456 EndZ=0
    g2: LineSegment StartX=-0.77 StartY=0.44456 StartZ=0 EndX=-0.77 EndY=-0.44456 EndZ=0
    g3: LineSegment StartX=-0.77 StartY=-0.44456 StartZ=0 EndX=3.85628e-11 EndY=-0.889119 EndZ=0
    g4: LineSegment StartX=3.85628e-11 StartY=-0.889119 StartZ=0 EndX=0.77 EndY=-0.44456 EndZ=0
    g5: LineSegment StartX=0.77 StartY=-0.44456 StartZ=0 EndX=0.77 EndY=0.44456 EndZ=0
    g6: Circle [constr] CenterX=0 CenterY=0 CenterZ=0 NormalX=0 NormalY=0 NormalZ=1 AngleXU=0 Radius=0.889119
  constraints (16):
    c: Coincident(g0,g1)
    c: Coincident(g1,g2)
    c: Coincident(g2,g3)
    c: Coincident(g3,g4)
    c: Coincident(g4,g5)
    c: Coincident(g5,g0)
    c: Equal(g0, g1-g5) x5
    c: PointOnObject(g0,g6)
    c: PointOnObject(g1,g6)
    c: PointOnObject(g2,g6)
    c: PointOnObject(g3,g6)
    c: PointOnObject(g4,g6)
    c: PointOnObject(g5,g6)
    c: Coincident(g6,g-1)
    c: PointOnObject(g0,g-2)
    c: DistanceX(g1,g0) = 1.54
FEATURE [PartDesign::Pocket] Pocket537  label="M3x8 Wrench071"
  BaseFeature = -> Pad617
  Length = 1
  Length2 = 100
  Profile = -> Sketch1487
  Type = 0
FEATURE [PartDesign::Chamfer] Chamfer294  label="M3x8 Smooth075"
  Base = -> Pocket537 [Face11,Edge2,Edge24,Edge3]
  BaseFeature = -> Pocket537
  Size = 0.2
FEATURE [PartDesign::Body] Body391  label="M2x060"
  Group = -> [Sketch1472,Pad623,Sketch1481,Pad617,Sketch1487,Pocket537,Chamfer294]
  Origin = -> Origin556
  Tip = -> Chamfer294
FEATURE [App::Part] Part139  label="M041"
  Group = -> [Body391,Body357]
  Origin = -> Origin517
  Placement = pos=(-9.1,-5.25,80) rot=(0,1,0;3.14159rad)
FEATURE [Sketcher::SketchObject] Sketch1488
  MapMode = 5
  Support = -> [XY_Plane508]
FEATURE [Sketcher::SketchObject] Sketch1489
  MapMode = 5
  Placement = pos=(0,0,2) rot=(0,0,1;0rad)
  Support = -> [Pad602]
  sketch-geometry (1):
    g0: Circle CenterX=0 CenterY=0 CenterZ=0 NormalX=0 NormalY=0 NormalZ=1 AngleXU=0 Radius=1
  constraints (2):
    c: Coincident(g0,g-1)
    c: Radius(g0) = 1
FEATURE [PartDesign::Pad] Pad637  label="M3x8 Thread078"
  BaseFeature = -> Pad602
  Length = 8
  Length2 = 100
  Profile = -> Sketch1489
  Type = 0
FEATURE [Sketcher::SketchObject] Sketch1490
  MapMode = 5
  Support = -> [XY_Plane531]
FEATURE [Sketcher::SketchObject] Sketch1491
  MapMode = 5
  Support = -> [XY_Plane435]
FEATURE [Sketcher::SketchObject] Sketch1493
  MapMode = 5
  Support = -> [XY_Plane435]
  sketch-geometry (8):
    g0: LineSegment StartX=0 StartY=2.3094 StartZ=0 EndX=-2 EndY=1.1547 EndZ=0
    g1: LineSegment StartX=-2 StartY=1.1547 StartZ=0 EndX=-2 EndY=-1.1547 EndZ=0
    g2: LineSegment StartX=-2 StartY=-1.1547 StartZ=0 EndX=-2e-16 EndY=-2.3094 EndZ=0
    g3: LineSegment StartX=-2e-16 StartY=-2.3094 StartZ=0 EndX=2 EndY=-1.1547 EndZ=0
    g4: LineSegment StartX=2 StartY=-1.1547 StartZ=0 EndX=2 EndY=1.1547 EndZ=0
    g5: LineSegment StartX=2 StartY=1.1547 StartZ=0 EndX=0 EndY=2.3094 EndZ=0
    g6: Circle [constr] CenterX=0 CenterY=0 CenterZ=0 NormalX=0 NormalY=0 NormalZ=1 AngleXU=0 Radius=2.3094
    g7: Circle CenterX=0 CenterY=0 CenterZ=0 NormalX=0 NormalY=0 NormalZ=1 AngleXU=0 Radius=1
  constraints (18):
    c: Coincident(g0,g1)
    c: Coincident(g1,g2)
    c: Coincident(g2,g3)
    c: Coincident(g3,g4)
    c: Coincident(g4,g5)
    c: Coincident(g5,g0)
    c: Equal(g0, g1-g5) x5
    c: PointOnObject(g0,g6)
    c: PointOnObject(g1,g6)
    c: PointOnObject(g2,g6)
    c: PointOnObject(g3,g6)
    c: PointOnObject(g4,g6)
    c: PointOnObject(g5,g6)
    c: Coincident(g6,g-1)
    c: PointOnObject(g5,g-2)
    c: DistanceX(g0,g4) = 4
    c: Coincident(g7,g-1)
    c: Radius(g7) = 1
FEATURE [PartDesign::Pad] Pad592  label="M3 Nut Primitive114"
  Length = 0.6
  Length2 = 0.6
  Profile = -> Sketch1493
  Type = 4
FEATURE [Sketcher::SketchObject] Sketch1485
  ExternalGeometry = -> [Pad592]
  MapMode = 5
  Placement = pos=(0,0,0) rot=(0.57735,0.57735,0.57735;2.0944rad)
  Support = -> [YZ_Plane443]
  sketch-geometry (6):
    g0: LineSegment StartX=-1.9594 StartY=0.6 StartZ=0 EndX=-2.8094 EndY=0.6 EndZ=0
    g1: LineSegment StartX=-2.8094 StartY=0.6 StartZ=0 EndX=-2.8094 EndY=-0.6 EndZ=0
    g2: LineSegment StartX=-2.8094 StartY=-0.6 StartZ=0 EndX=-1.9594 EndY=-0.6 EndZ=0
    g3: LineSegment StartX=-1.9594 StartY=-0.6 StartZ=0 EndX=-2.3094 EndY=-0.4 EndZ=0
    g4: LineSegment StartX=-2.3094 StartY=-0.4 StartZ=0 EndX=-2.3094 EndY=0.4 EndZ=0
    g5: LineSegment StartX=-2.3094 StartY=0.4 StartZ=0 EndX=-1.9594 EndY=0.6 EndZ=0
  constraints (15):
    c: Horizontal(g0)
    c: Coincident(g0,g1)
    c: Coincident(g1,g2)
    c: Coincident(g2,g3)
    c: Coincident(g3,g4)
    c: Coincident(g4,g5)
    c: Coincident(g5,g0)
    c: Symmetric(g4,g3,g-1)
    c: Symmetric(g0,g2,g-1)
    c: Symmetric(g1,g0,g-1)
    c: DistanceX(g0,g4) = 0.5
    c: DistanceY(g3,g4) = 0.8
    c: DistanceY(g1,g0) = 1.2
    c: PointOnObject(g3,g-3)
    c: DistanceX(g4,g0) = 0.35
FEATURE [PartDesign::Groove] Groove123  label="M3 Nut Smooth117"
  Angle = 360
  Axis = (-2e-16,3e-16,1)
  Base = (0,0,0)
  BaseFeature = -> Pad592
  Profile = -> Sketch1485
  ReferenceAxis = -> Sketch1485 [V_Axis]
  Reversed = true
FEATURE [PartDesign::Chamfer] Chamfer231  label="M3 Nut Smooth Hole097"
  Base = -> Groove123 [Edge24,Edge23]
  BaseFeature = -> Groove123
  Size = 0.2
FEATURE [Sketcher::SketchObject] Sketch1494
  MapMode = 5
  Support = -> [XY_Plane436]
  sketch-geometry (1):
    g0: Circle CenterX=0 CenterY=0 CenterZ=0 NormalX=0 NormalY=0 NormalZ=1 AngleXU=0 Radius=1.9
  constraints (2):
    c: Coincident(g0,g-1)
    c: Radius(g0) = 1.9
FEATURE [PartDesign::Pad] Pad627  label="M3x8 Head077"
  Length = 2
  Length2 = 100
  Profile = -> Sketch1494
  Type = 0
FEATURE [Sketcher::SketchObject] Sketch1234
  MapMode = 5
  Placement = pos=(0,0,2) rot=(0,0,1;0rad)
  Support = -> [Pad627]
  sketch-geometry (1):
    g0: Circle CenterX=0 CenterY=0 CenterZ=0 NormalX=0 NormalY=0 NormalZ=1 AngleXU=0 Radius=1
  constraints (2):
    c: Coincident(g0,g-1)
    c: Radius(g0) = 1
FEATURE [PartDesign::Pad] Pad624  label="M3x8 Thread073"
  BaseFeature = -> Pad627
  Length = 8
  Length2 = 100
  Profile = -> Sketch1234
  Type = 0
FEATURE [Sketcher::SketchObject] Sketch1477
  MapMode = 5
  Placement = pos=(0,0,0) rot=(1,0,0;3.14159rad)
  Support = -> [Pad624]
  sketch-geometry (7):
    g0: LineSegment StartX=0.77 StartY=0.44456 StartZ=0 EndX=0 EndY=0.889119 EndZ=0
    g1: LineSegment StartX=0 StartY=0.889119 StartZ=0 EndX=-0.77 EndY=0.44456 EndZ=0
    g2: LineSegment StartX=-0.77 StartY=0.44456 StartZ=0 EndX=-0.77 EndY=-0.44456 EndZ=0
    g3: LineSegment StartX=-0.77 StartY=-0.44456 StartZ=0 EndX=3.85628e-11 EndY=-0.889119 EndZ=0
    g4: LineSegment StartX=3.85628e-11 StartY=-0.889119 StartZ=0 EndX=0.77 EndY=-0.44456 EndZ=0
    g5: LineSegment StartX=0.77 StartY=-0.44456 StartZ=0 EndX=0.77 EndY=0.44456 EndZ=0
    g6: Circle [constr] CenterX=0 CenterY=0 CenterZ=0 NormalX=0 NormalY=0 NormalZ=1 AngleXU=0 Radius=0.889119
  constraints (16):
    c: Coincident(g0,g1)
    c: Coincident(g1,g2)
    c: Coincident(g2,g3)
    c: Coincident(g3,g4)
    c: Coincident(g4,g5)
    c: Coincident(g5,g0)
    c: Equal(g0, g1-g5) x5
    c: PointOnObject(g0,g6)
    c: PointOnObject(g1,g6)
    c: PointOnObject(g2,g6)
    c: PointOnObject(g3,g6)
    c: PointOnObject(g4,g6)
    c: PointOnObject(g5,g6)
    c: Coincident(g6,g-1)
    c: PointOnObject(g0,g-2)
    c: DistanceX(g1,g0) = 1.54
FEATURE [PartDesign::Pocket] Pocket536  label="M3x8 Wrench070"
  BaseFeature = -> Pad624
  Length = 1
  Length2 = 100
  Profile = -> Sketch1477
  Type = 0
FEATURE [PartDesign::Chamfer] Chamfer297  label="M3x8 Smooth077"
  Base = -> Pocket536 [Face11,Edge2,Edge24,Edge3]
  BaseFeature = -> Pocket536
  Size = 0.2
FEATURE [PartDesign::Body] Body370  label="M2x056"
  Group = -> [Sketch1494,Pad627,Sketch1234,Pad624,Sketch1477,Pocket536,Chamfer297]
  Origin = -> Origin564
  Tip = -> Chamfer297
FEATURE [Sketcher::SketchObject] Sketch1495
  MapMode = 5
  Support = -> [XY_Plane508]
FEATURE [Sketcher::SketchObject] Sketch1497
  MapMode = 5
  Support = -> [XY_Plane539]
  sketch-geometry (1):
    g0: Circle CenterX=0 CenterY=0 CenterZ=0 NormalX=0 NormalY=0 NormalZ=1 AngleXU=0 Radius=2.75
  constraints (2):
    c: Coincident(g0,g-1)
    c: Radius(g0) = 2.75
FEATURE [PartDesign::Pad] Pad619  label="M3x8 Head074"
  Length = 3
  Length2 = 100
  Profile = -> Sketch1497
  Type = 0
FEATURE [Sketcher::SketchObject] Sketch1199
  MapMode = 5
  Placement = pos=(0,0,3) rot=(0,0,1;0rad)
  Support = -> [Pad619]
  sketch-geometry (1):
    g0: Circle CenterX=0 CenterY=0 CenterZ=0 NormalX=0 NormalY=0 NormalZ=1 AngleXU=0 Radius=1.5
  constraints (2):
    c: Coincident(g0,g-1)
    c: Radius(g0) = 1.5
FEATURE [PartDesign::Pad] Pad631  label="M3x8 Thread076"
  BaseFeature = -> Pad619
  Length = 8
  Length2 = 100
  Profile = -> Sketch1199
  Type = 0
FEATURE [Sketcher::SketchObject] Sketch1179
  MapMode = 5
  Placement = pos=(0,0,0) rot=(1,0,0;3.14159rad)
  Support = -> [Pad631]
  sketch-geometry (7):
    g0: LineSegment StartX=1.275 StartY=0.736122 StartZ=0 EndX=0 EndY=1.47224 EndZ=0
    g1: LineSegment StartX=0 StartY=1.47224 StartZ=0 EndX=-1.275 EndY=0.736122 EndZ=0
    g2: LineSegment StartX=-1.275 StartY=0.736122 StartZ=0 EndX=-1.275 EndY=-0.736122 EndZ=0
    g3: LineSegment StartX=-1.275 StartY=-0.736122 StartZ=0 EndX=1.34766e-11 EndY=-1.47224 EndZ=0
    g4: LineSegment StartX=1.34766e-11 StartY=-1.47224 StartZ=0 EndX=1.275 EndY=-0.736122 EndZ=0
    g5: LineSegment StartX=1.275 StartY=-0.736122 StartZ=0 EndX=1.275 EndY=0.736122 EndZ=0
    g6: Circle [constr] CenterX=0 CenterY=0 CenterZ=0 NormalX=0 NormalY=0 NormalZ=1 AngleXU=0 Radius=1.47224
  constraints (16):
    c: Coincident(g0,g1)
    c: Coincident(g1,g2)
    c: Coincident(g2,g3)
    c: Coincident(g3,g4)
    c: Coincident(g4,g5)
    c: Coincident(g5,g0)
    c: Equal(g0, g1-g5) x5
    c: PointOnObject(g0,g6)
    c: PointOnObject(g1,g6)
    c: PointOnObject(g2,g6)
    c: PointOnObject(g3,g6)
    c: PointOnObject(g4,g6)
    c: PointOnObject(g5,g6)
    c: Coincident(g6,g-1)
    c: PointOnObject(g0,g-2)
    c: DistanceX(g1,g0) = 2.55
FEATURE [PartDesign::Pocket] Pocket542  label="M3x8 Wrench074"
  BaseFeature = -> Pad631
  Length = 1.3
  Length2 = 100
  Profile = -> Sketch1179
  Type = 0
FEATURE [PartDesign::Chamfer] Chamfer264  label="M3x8 Smooth066"
  Base = -> Pocket542 [Face11,Edge2,Edge24,Edge3]
  BaseFeature = -> Pocket542
  Size = 0.2
FEATURE [PartDesign::Body] Body378  label="M3x081"
  Group = -> [Sketch1497,Pad619,Sketch1199,Pad631,Sketch1179,Pocket542,Chamfer264]
  Origin = -> Origin559
  Placement = pos=(14.15,14.15,-6) rot=(0,0,1;0rad)
  Tip = -> Chamfer264
FEATURE [Sketcher::SketchObject] Sketch1498
  MapMode = 5
  Placement = pos=(0,0,2) rot=(0,0,1;0rad)
  Support = -> [Pad603]
  sketch-geometry (1):
    g0: Circle CenterX=0 CenterY=0 CenterZ=0 NormalX=0 NormalY=0 NormalZ=1 AngleXU=0 Radius=1
  constraints (2):
    c: Coincident(g0,g-1)
    c: Radius(g0) = 1
FEATURE [PartDesign::Pad] Pad591  label="M3x8 Thread067"
  BaseFeature = -> Pad603
  Length = 8
  Length2 = 100
  Profile = -> Sketch1498
  Type = 0
FEATURE [Sketcher::SketchObject] Sketch1482
  MapMode = 5
  Placement = pos=(0,0,0) rot=(1,0,0;3.14159rad)
  Support = -> [Pad591]
  sketch-geometry (7):
    g0: LineSegment StartX=0.77 StartY=0.44456 StartZ=0 EndX=0 EndY=0.889119 EndZ=0
    g1: LineSegment StartX=0 StartY=0.889119 StartZ=0 EndX=-0.77 EndY=0.44456 EndZ=0
    g2: LineSegment StartX=-0.77 StartY=0.44456 StartZ=0 EndX=-0.77 EndY=-0.44456 EndZ=0
    g3: LineSegment StartX=-0.77 StartY=-0.44456 StartZ=0 EndX=3.85628e-11 EndY=-0.889119 EndZ=0
    g4: LineSegment StartX=3.85628e-11 StartY=-0.889119 StartZ=0 EndX=0.77 EndY=-0.44456 EndZ=0
    g5: LineSegment StartX=0.77 StartY=-0.44456 StartZ=0 EndX=0.77 EndY=0.44456 EndZ=0
    g6: Circle [constr] CenterX=0 CenterY=0 CenterZ=0 NormalX=0 NormalY=0 NormalZ=1 AngleXU=0 Radius=0.889119
  constraints (16):
    c: Coincident(g0,g1)
    c: Coincident(g1,g2)
    c: Coincident(g2,g3)
    c: Coincident(g3,g4)
    c: Coincident(g4,g5)
    c: Coincident(g5,g0)
    c: Equal(g0, g1-g5) x5
    c: PointOnObject(g0,g6)
    c: PointOnObject(g1,g6)
    c: PointOnObject(g2,g6)
    c: PointOnObject(g3,g6)
    c: PointOnObject(g4,g6)
    c: PointOnObject(g5,g6)
    c: Coincident(g6,g-1)
    c: PointOnObject(g0,g-2)
    c: DistanceX(g1,g0) = 1.54
FEATURE [PartDesign::Pocket] Pocket532  label="M3x8 Wrench068"
  BaseFeature = -> Pad591
  Length = 1
  Length2 = 100
  Profile = -> Sketch1482
  Type = 0
FEATURE [PartDesign::Chamfer] Chamfer223  label="M3x8 Smooth058"
  Base = -> Pocket532 [Face11,Edge2,Edge24,Edge3]
  BaseFeature = -> Pocket532
  Size = 0.2
FEATURE [PartDesign::Body] Body353  label="M2x054"
  Group = -> [Sketch1181,Pad603,Sketch1498,Pad591,Sketch1482,Pocket532,Chamfer223]
  Origin = -> Origin563
  Placement = pos=(-28.75,10,15) rot=(0,1,0;1.5708rad)
  Tip = -> Chamfer223
FEATURE [Sketcher::SketchObject] Sketch1499
  ExternalGeometry = -> [Pad639]
  MapMode = 5
  Placement = pos=(0,0,0) rot=(0.57735,0.57735,0.57735;2.0944rad)
  Support = -> [YZ_Plane441]
  sketch-geometry (6):
    g0: LineSegment StartX=-1.9594 StartY=0.6 StartZ=0 EndX=-2.8094 EndY=0.6 EndZ=0
    g1: LineSegment StartX=-2.8094 StartY=0.6 StartZ=0 EndX=-2.8094 EndY=-0.6 EndZ=0
    g2: LineSegment StartX=-2.8094 StartY=-0.6 StartZ=0 EndX=-1.9594 EndY=-0.6 EndZ=0
    g3: LineSegment StartX=-1.9594 StartY=-0.6 StartZ=0 EndX=-2.3094 EndY=-0.4 EndZ=0
    g4: LineSegment StartX=-2.3094 StartY=-0.4 StartZ=0 EndX=-2.3094 EndY=0.4 EndZ=0
    g5: LineSegment StartX=-2.3094 StartY=0.4 StartZ=0 EndX=-1.9594 EndY=0.6 EndZ=0
  constraints (15):
    c: Horizontal(g0)
    c: Coincident(g0,g1)
    c: Coincident(g1,g2)
    c: Coincident(g2,g3)
    c: Coincident(g3,g4)
    c: Coincident(g4,g5)
    c: Coincident(g5,g0)
    c: Symmetric(g4,g3,g-1)
    c: Symmetric(g0,g2,g-1)
    c: Symmetric(g1,g0,g-1)
    c: DistanceX(g0,g4) = 0.5
    c: DistanceY(g3,g4) = 0.8
    c: DistanceY(g1,g0) = 1.2
    c: PointOnObject(g3,g-3)
    c: DistanceX(g4,g0) = 0.35
FEATURE [PartDesign::Groove] Groove121  label="M3 Nut Smooth115"
  Angle = 360
  Axis = (-2e-16,3e-16,1)
  Base = (0,0,0)
  BaseFeature = -> Pad639
  Profile = -> Sketch1499
  ReferenceAxis = -> Sketch1499 [V_Axis]
  Reversed = true
FEATURE [PartDesign::Chamfer] Chamfer221  label="M3 Nut Smooth Hole093"
  Base = -> Groove121 [Edge24,Edge23]
  BaseFeature = -> Groove121
  Size = 0.2
FEATURE [Sketcher::SketchObject] Sketch1500
  MapMode = 5
  Placement = pos=(0,0,0) rot=(1,0,0;3.14159rad)
  Support = -> [Pad637]
  sketch-geometry (7):
    g0: LineSegment StartX=0.77 StartY=0.44456 StartZ=0 EndX=0 EndY=0.889119 EndZ=0
    g1: LineSegment StartX=0 StartY=0.889119 StartZ=0 EndX=-0.77 EndY=0.44456 EndZ=0
    g2: LineSegment StartX=-0.77 StartY=0.44456 StartZ=0 EndX=-0.77 EndY=-0.44456 EndZ=0
    g3: LineSegment StartX=-0.77 StartY=-0.44456 StartZ=0 EndX=3.85628e-11 EndY=-0.889119 EndZ=0
    g4: LineSegment StartX=3.85628e-11 StartY=-0.889119 StartZ=0 EndX=0.77 EndY=-0.44456 EndZ=0
    g5: LineSegment StartX=0.77 StartY=-0.44456 StartZ=0 EndX=0.77 EndY=0.44456 EndZ=0
    g6: Circle [constr] CenterX=0 CenterY=0 CenterZ=0 NormalX=0 NormalY=0 NormalZ=1 AngleXU=0 Radius=0.889119
  constraints (16):
    c: Coincident(g0,g1)
    c: Coincident(g1,g2)
    c: Coincident(g2,g3)
    c: Coincident(g3,g4)
    c: Coincident(g4,g5)
    c: Coincident(g5,g0)
    c: Equal(g0, g1-g5) x5
    c: PointOnObject(g0,g6)
    c: PointOnObject(g1,g6)
    c: PointOnObject(g2,g6)
    c: PointOnObject(g3,g6)
    c: PointOnObject(g4,g6)
    c: PointOnObject(g5,g6)
    c: Coincident(g6,g-1)
    c: PointOnObject(g0,g-2)
    c: DistanceX(g1,g0) = 1.54
FEATURE [PartDesign::Pocket] Pocket539  label="M3x8 Wrench072"
  BaseFeature = -> Pad637
  Length = 1
  Length2 = 100
  Profile = -> Sketch1500
  Type = 0
FEATURE [PartDesign::Chamfer] Chamfer239  label="M3x8 Smooth062"
  Base = -> Pocket539 [Face11,Edge2,Edge24,Edge3]
  BaseFeature = -> Pocket539
  Size = 0.2
FEATURE [Sketcher::SketchObject] Sketch1501
  MapMode = 5
  Support = -> [XY_Plane435]
FEATURE [PartDesign::Body] Body397  label="M2 Nut051"
  Group = -> [Sketch1493,Pad592,Sketch1485,Groove123,Chamfer231,Sketch1491,Sketch1501]
  Origin = -> Origin429
  Placement = pos=(0,0,2.75) rot=(0,0,1;0rad)
  Tip = -> Chamfer231
FEATURE [Sketcher::SketchObject] Sketch1503
  MapMode = 5
  Support = -> [XY_Plane419]
  sketch-geometry (8):
    g0: LineSegment StartX=0 StartY=2.3094 StartZ=0 EndX=-2 EndY=1.1547 EndZ=0
    g1: LineSegment StartX=-2 StartY=1.1547 StartZ=0 EndX=-2 EndY=-1.1547 EndZ=0
    g2: LineSegment StartX=-2 StartY=-1.1547 StartZ=0 EndX=-2e-16 EndY=-2.3094 EndZ=0
    g3: LineSegment StartX=-2e-16 StartY=-2.3094 StartZ=0 EndX=2 EndY=-1.1547 EndZ=0
    g4: LineSegment StartX=2 StartY=-1.1547 StartZ=0 EndX=2 EndY=1.1547 EndZ=0
    g5: LineSegment StartX=2 StartY=1.1547 StartZ=0 EndX=0 EndY=2.3094 EndZ=0
    g6: Circle [constr] CenterX=0 CenterY=0 CenterZ=0 NormalX=0 NormalY=0 NormalZ=1 AngleXU=0 Radius=2.3094
    g7: Circle CenterX=0 CenterY=0 CenterZ=0 NormalX=0 NormalY=0 NormalZ=1 AngleXU=0 Radius=1
  constraints (18):
    c: Coincident(g0,g1)
    c: Coincident(g1,g2)
    c: Coincident(g2,g3)
    c: Coincident(g3,g4)
    c: Coincident(g4,g5)
    c: Coincident(g5,g0)
    c: Equal(g0, g1-g5) x5
    c: PointOnObject(g0,g6)
    c: PointOnObject(g1,g6)
    c: PointOnObject(g2,g6)
    c: PointOnObject(g3,g6)
    c: PointOnObject(g4,g6)
    c: PointOnObject(g5,g6)
    c: Coincident(g6,g-1)
    c: PointOnObject(g5,g-2)
    c: DistanceX(g0,g4) = 4
    c: Coincident(g7,g-1)
    c: Radius(g7) = 1
FEATURE [PartDesign::Pad] Pad628  label="M3 Nut Primitive117"
  Length = 0.6
  Length2 = 0.6
  Profile = -> Sketch1503
  Type = 4
FEATURE [Sketcher::SketchObject] Sketch1184
  ExternalGeometry = -> [Pad628]
  MapMode = 5
  Placement = pos=(0,0,0) rot=(0.57735,0.57735,0.57735;2.0944rad)
  Support = -> [YZ_Plane533]
  sketch-geometry (6):
    g0: LineSegment StartX=-1.9594 StartY=0.6 StartZ=0 EndX=-2.8094 EndY=0.6 EndZ=0
    g1: LineSegment StartX=-2.8094 StartY=0.6 StartZ=0 EndX=-2.8094 EndY=-0.6 EndZ=0
    g2: LineSegment StartX=-2.8094 StartY=-0.6 StartZ=0 EndX=-1.9594 EndY=-0.6 EndZ=0
    g3: LineSegment StartX=-1.9594 StartY=-0.6 StartZ=0 EndX=-2.3094 EndY=-0.4 EndZ=0
    g4: LineSegment StartX=-2.3094 StartY=-0.4 StartZ=0 EndX=-2.3094 EndY=0.4 EndZ=0
    g5: LineSegment StartX=-2.3094 StartY=0.4 StartZ=0 EndX=-1.9594 EndY=0.6 EndZ=0
  constraints (15):
    c: Horizontal(g0)
    c: Coincident(g0,g1)
    c: Coincident(g1,g2)
    c: Coincident(g2,g3)
    c: Coincident(g3,g4)
    c: Coincident(g4,g5)
    c: Coincident(g5,g0)
    c: Symmetric(g4,g3,g-1)
    c: Symmetric(g0,g2,g-1)
    c: Symmetric(g1,g0,g-1)
    c: DistanceX(g0,g4) = 0.5
    c: DistanceY(g3,g4) = 0.8
    c: DistanceY(g1,g0) = 1.2
    c: PointOnObject(g3,g-3)
    c: DistanceX(g4,g0) = 0.35
FEATURE [PartDesign::Groove] Groove126  label="M3 Nut Smooth120"
  Angle = 360
  Axis = (-2e-16,3e-16,1)
  Base = (0,0,0)
  BaseFeature = -> Pad628
  Profile = -> Sketch1184
  ReferenceAxis = -> Sketch1184 [V_Axis]
  Reversed = true
FEATURE [PartDesign::Chamfer] Chamfer228  label="M3 Nut Smooth Hole096"
  Base = -> Groove126 [Edge24,Edge23]
  BaseFeature = -> Groove126
  Size = 0.2
FEATURE [Sketcher::SketchObject] Sketch1504
  MapMode = 5
  Support = -> [XY_Plane531]
  sketch-geometry (8):
    g0: LineSegment StartX=0 StartY=2.3094 StartZ=0 EndX=-2 EndY=1.1547 EndZ=0
    g1: LineSegment StartX=-2 StartY=1.1547 StartZ=0 EndX=-2 EndY=-1.1547 EndZ=0
    g2: LineSegment StartX=-2 StartY=-1.1547 StartZ=0 EndX=-2e-16 EndY=-2.3094 EndZ=0
    g3: LineSegment StartX=-2e-16 StartY=-2.3094 StartZ=0 EndX=2 EndY=-1.1547 EndZ=0
    g4: LineSegment StartX=2 StartY=-1.1547 StartZ=0 EndX=2 EndY=1.1547 EndZ=0
    g5: LineSegment StartX=2 StartY=1.1547 StartZ=0 EndX=0 EndY=2.3094 EndZ=0
    g6: Circle [constr] CenterX=0 CenterY=0 CenterZ=0 NormalX=0 NormalY=0 NormalZ=1 AngleXU=0 Radius=2.3094
    g7: Circle CenterX=0 CenterY=0 CenterZ=0 NormalX=0 NormalY=0 NormalZ=1 AngleXU=0 Radius=1
  constraints (18):
    c: Coincident(g0,g1)
    c: Coincident(g1,g2)
    c: Coincident(g2,g3)
    c: Coincident(g3,g4)
    c: Coincident(g4,g5)
    c: Coincident(g5,g0)
    c: Equal(g0, g1-g5) x5
    c: PointOnObject(g0,g6)
    c: PointOnObject(g1,g6)
    c: PointOnObject(g2,g6)
    c: PointOnObject(g3,g6)
    c: PointOnObject(g4,g6)
    c: PointOnObject(g5,g6)
    c: Coincident(g6,g-1)
    c: PointOnObject(g5,g-2)
    c: DistanceX(g0,g4) = 4
    c: Coincident(g7,g-1)
    c: Radius(g7) = 1
FEATURE [PartDesign::Pad] Pad610  label="M3 Nut Primitive116"
  Length = 0.6
  Length2 = 0.6
  Profile = -> Sketch1504
  Type = 4
FEATURE [Sketcher::SketchObject] Sketch1502
  ExternalGeometry = -> [Pad610]
  MapMode = 5
  Placement = pos=(0,0,0) rot=(0.57735,0.57735,0.57735;2.0944rad)
  Support = -> [YZ_Plane413]
  sketch-geometry (6):
    g0: LineSegment StartX=-1.9594 StartY=0.6 StartZ=0 EndX=-2.8094 EndY=0.6 EndZ=0
    g1: LineSegment StartX=-2.8094 StartY=0.6 StartZ=0 EndX=-2.8094 EndY=-0.6 EndZ=0
    g2: LineSegment StartX=-2.8094 StartY=-0.6 StartZ=0 EndX=-1.9594 EndY=-0.6 EndZ=0
    g3: LineSegment StartX=-1.9594 StartY=-0.6 StartZ=0 EndX=-2.3094 EndY=-0.4 EndZ=0
    g4: LineSegment StartX=-2.3094 StartY=-0.4 StartZ=0 EndX=-2.3094 EndY=0.4 EndZ=0
    g5: LineSegment StartX=-2.3094 StartY=0.4 StartZ=0 EndX=-1.9594 EndY=0.6 EndZ=0
  constraints (15):
    c: Horizontal(g0)
    c: Coincident(g0,g1)
    c: Coincident(g1,g2)
    c: Coincident(g2,g3)
    c: Coincident(g3,g4)
    c: Coincident(g4,g5)
    c: Coincident(g5,g0)
    c: Symmetric(g4,g3,g-1)
    c: Symmetric(g0,g2,g-1)
    c: Symmetric(g1,g0,g-1)
    c: DistanceX(g0,g4) = 0.5
    c: DistanceY(g3,g4) = 0.8
    c: DistanceY(g1,g0) = 1.2
    c: PointOnObject(g3,g-3)
    c: DistanceX(g4,g0) = 0.35
FEATURE [PartDesign::Groove] Groove127  label="M3 Nut Smooth121"
  Angle = 360
  Axis = (-2e-16,3e-16,1)
  Base = (0,0,0)
  BaseFeature = -> Pad610
  Profile = -> Sketch1502
  ReferenceAxis = -> Sketch1502 [V_Axis]
  Reversed = true
FEATURE [PartDesign::Chamfer] Chamfer288  label="M3 Nut Smooth Hole123"
  Base = -> Groove127 [Edge24,Edge23]
  BaseFeature = -> Groove127
  Size = 0.2
FEATURE [PartDesign::Body] Body372  label="M2 Nut050"
  Group = -> [Sketch1504,Pad610,Sketch1502,Groove127,Chamfer288,Sketch1271,Sketch1490]
  Origin = -> Origin549
  Placement = pos=(0,0,2.75) rot=(0,0,1;0rad)
  Tip = -> Chamfer288
FEATURE [Sketcher::SketchObject] Sketch1506
  MapMode = 5
  Support = -> [XY_Plane441]
  sketch-geometry (1):
    g0: Circle CenterX=0 CenterY=0 CenterZ=0 NormalX=0 NormalY=0 NormalZ=1 AngleXU=0 Radius=1.9
  constraints (2):
    c: Coincident(g0,g-1)
    c: Radius(g0) = 1.9
FEATURE [PartDesign::Pad] Pad622  label="M3x8 Head075"
  Length = 2
  Length2 = 100
  Profile = -> Sketch1506
  Type = 0
FEATURE [Sketcher::SketchObject] Sketch1496
  MapMode = 5
  Placement = pos=(0,0,2) rot=(0,0,1;0rad)
  Support = -> [Pad622]
  sketch-geometry (1):
    g0: Circle CenterX=0 CenterY=0 CenterZ=0 NormalX=0 NormalY=0 NormalZ=1 AngleXU=0 Radius=1
  constraints (2):
    c: Coincident(g0,g-1)
    c: Radius(g0) = 1
FEATURE [PartDesign::Pad] Pad632  label="M3x8 Thread077"
  BaseFeature = -> Pad622
  Length = 8
  Length2 = 100
  Profile = -> Sketch1496
  Type = 0
FEATURE [Sketcher::SketchObject] Sketch1492
  MapMode = 5
  Placement = pos=(0,0,0) rot=(1,0,0;3.14159rad)
  Support = -> [Pad632]
  sketch-geometry (7):
    g0: LineSegment StartX=0.77 StartY=0.44456 StartZ=0 EndX=0 EndY=0.889119 EndZ=0
    g1: LineSegment StartX=0 StartY=0.889119 StartZ=0 EndX=-0.77 EndY=0.44456 EndZ=0
    g2: LineSegment StartX=-0.77 StartY=0.44456 StartZ=0 EndX=-0.77 EndY=-0.44456 EndZ=0
    g3: LineSegment StartX=-0.77 StartY=-0.44456 StartZ=0 EndX=3.85628e-11 EndY=-0.889119 EndZ=0
    g4: LineSegment StartX=3.85628e-11 StartY=-0.889119 StartZ=0 EndX=0.77 EndY=-0.44456 EndZ=0
    g5: LineSegment StartX=0.77 StartY=-0.44456 StartZ=0 EndX=0.77 EndY=0.44456 EndZ=0
    g6: Circle [constr] CenterX=0 CenterY=0 CenterZ=0 NormalX=0 NormalY=0 NormalZ=1 AngleXU=0 Radius=0.889119
  constraints (16):
    c: Coincident(g0,g1)
    c: Coincident(g1,g2)
    c: Coincident(g2,g3)
    c: Coincident(g3,g4)
    c: Coincident(g4,g5)
    c: Coincident(g5,g0)
    c: Equal(g0, g1-g5) x5
    c: PointOnObject(g0,g6)
    c: PointOnObject(g1,g6)
    c: PointOnObject(g2,g6)
    c: PointOnObject(g3,g6)
    c: PointOnObject(g4,g6)
    c: PointOnObject(g5,g6)
    c: Coincident(g6,g-1)
    c: PointOnObject(g0,g-2)
    c: DistanceX(g1,g0) = 1.54
FEATURE [PartDesign::Pocket] Pocket543  label="M3x8 Wrench075"
  BaseFeature = -> Pad632
  Length = 1
  Length2 = 100
  Profile = -> Sketch1492
  Type = 0
FEATURE [PartDesign::Chamfer] Chamfer250  label="M3x8 Smooth064"
  Base = -> Pocket543 [Face11,Edge2,Edge24,Edge3]
  BaseFeature = -> Pocket543
  Size = 0.2
FEATURE [PartDesign::Body] Body382  label="M2x057"
  Group = -> [Sketch1506,Pad622,Sketch1496,Pad632,Sketch1492,Pocket543,Chamfer250]
  Origin = -> Origin430
  Tip = -> Chamfer250
FEATURE [App::Part] Part157  label="M049"
  Group = -> [Body382,Body372]
  Origin = -> Origin537
  Placement = pos=(-9.1,5.25,80) rot=(0,1,0;3.14159rad)
FEATURE [Sketcher::SketchObject] Sketch1507
  MapMode = 5
  Placement = pos=(0,0,3) rot=(0,0,1;0rad)
  Support = -> [Pad553]
  sketch-geometry (1):
    g0: Circle CenterX=0 CenterY=0 CenterZ=0 NormalX=0 NormalY=0 NormalZ=1 AngleXU=0 Radius=1.5
  constraints (2):
    c: Coincident(g0,g-1)
    c: Radius(g0) = 1.5
FEATURE [PartDesign::Pad] Pad567  label="M3x20 Thread046"
  BaseFeature = -> Pad553
  Length = 20
  Length2 = 100
  Profile = -> Sketch1507
  Type = 0
FEATURE [Sketcher::SketchObject] Sketch1218
  MapMode = 5
  Placement = pos=(0,0,0) rot=(1,0,0;3.14159rad)
  Support = -> [Pad567]
  sketch-geometry (7):
    g0: LineSegment StartX=1.275 StartY=0.736122 StartZ=0 EndX=0 EndY=1.47224 EndZ=0
    g1: LineSegment StartX=0 StartY=1.47224 StartZ=0 EndX=-1.275 EndY=0.736122 EndZ=0
    g2: LineSegment StartX=-1.275 StartY=0.736122 StartZ=0 EndX=-1.275 EndY=-0.736122 EndZ=0
    g3: LineSegment StartX=-1.275 StartY=-0.736122 StartZ=0 EndX=1.34766e-11 EndY=-1.47224 EndZ=0
    g4: LineSegment StartX=1.34766e-11 StartY=-1.47224 StartZ=0 EndX=1.275 EndY=-0.736122 EndZ=0
    g5: LineSegment StartX=1.275 StartY=-0.736122 StartZ=0 EndX=1.275 EndY=0.736122 EndZ=0
    g6: Circle [constr] CenterX=0 CenterY=0 CenterZ=0 NormalX=0 NormalY=0 NormalZ=1 AngleXU=0 Radius=1.47224
  constraints (16):
    c: Coincident(g0,g1)
    c: Coincident(g1,g2)
    c: Coincident(g2,g3)
    c: Coincident(g3,g4)
    c: Coincident(g4,g5)
    c: Coincident(g5,g0)
    c: Equal(g0, g1-g5) x5
    c: PointOnObject(g0,g6)
    c: PointOnObject(g1,g6)
    c: PointOnObject(g2,g6)
    c: PointOnObject(g3,g6)
    c: PointOnObject(g4,g6)
    c: PointOnObject(g5,g6)
    c: Coincident(g6,g-1)
    c: PointOnObject(g0,g-2)
    c: DistanceX(g1,g0) = 2.55
FEATURE [PartDesign::Pocket] Pocket511  label="M3x20 Wrench046"
  BaseFeature = -> Pad567
  Length = 1.3
  Length2 = 100
  Profile = -> Sketch1218
  Type = 0
FEATURE [PartDesign::Chamfer] Chamfer298  label="M3x20 Smooth054"
  Base = -> Pocket511 [Face11,Edge2,Edge24,Edge3]
  BaseFeature = -> Pocket511
  Size = 0.2
FEATURE [PartDesign::Body] Body360  label="M3x075"
  Group = -> [Sketch1220,Pad553,Sketch1507,Pad567,Sketch1218,Pocket511,Chamfer298]
  Origin = -> Origin568
  Placement = pos=(11.25,-55.6,224.85) rot=(0,-1,0;1.5708rad)
  Tip = -> Chamfer298
FEATURE [Sketcher::SketchObject] Sketch1508
  MapMode = 5
  Support = -> [XY_Plane429]
  sketch-geometry (1):
    g0: Circle CenterX=0 CenterY=0 CenterZ=0 NormalX=0 NormalY=0 NormalZ=1 AngleXU=0 Radius=2.75
  constraints (2):
    c: Coincident(g0,g-1)
    c: Radius(g0) = 2.75
FEATURE [PartDesign::Pad] Pad562  label="M3x20 Head045"
  Length = 3
  Length2 = 100
  Profile = -> Sketch1508
  Type = 0
FEATURE [Sketcher::SketchObject] Sketch1200
  MapMode = 5
  Placement = pos=(0,0,3) rot=(0,0,1;0rad)
  Support = -> [Pad562]
  sketch-geometry (1):
    g0: Circle CenterX=0 CenterY=0 CenterZ=0 NormalX=0 NormalY=0 NormalZ=1 AngleXU=0 Radius=1.5
  constraints (2):
    c: Coincident(g0,g-1)
    c: Radius(g0) = 1.5
FEATURE [PartDesign::Pad] Pad564  label="M3x20 Thread045"
  BaseFeature = -> Pad562
  Length = 20
  Length2 = 100
  Profile = -> Sketch1200
  Type = 0
FEATURE [Sketcher::SketchObject] Sketch1505
  MapMode = 5
  Placement = pos=(0,0,0) rot=(1,0,0;3.14159rad)
  Support = -> [Pad564]
  sketch-geometry (7):
    g0: LineSegment StartX=1.275 StartY=0.736122 StartZ=0 EndX=0 EndY=1.47224 EndZ=0
    g1: LineSegment StartX=0 StartY=1.47224 StartZ=0 EndX=-1.275 EndY=0.736122 EndZ=0
    g2: LineSegment StartX=-1.275 StartY=0.736122 StartZ=0 EndX=-1.275 EndY=-0.736122 EndZ=0
    g3: LineSegment StartX=-1.275 StartY=-0.736122 StartZ=0 EndX=1.34766e-11 EndY=-1.47224 EndZ=0
    g4: LineSegment StartX=1.34766e-11 StartY=-1.47224 StartZ=0 EndX=1.275 EndY=-0.736122 EndZ=0
    g5: LineSegment StartX=1.275 StartY=-0.736122 StartZ=0 EndX=1.275 EndY=0.736122 EndZ=0
    g6: Circle [constr] CenterX=0 CenterY=0 CenterZ=0 NormalX=0 NormalY=0 NormalZ=1 AngleXU=0 Radius=1.47224
  constraints (16):
    c: Coincident(g0,g1)
    c: Coincident(g1,g2)
    c: Coincident(g2,g3)
    c: Coincident(g3,g4)
    c: Coincident(g4,g5)
    c: Coincident(g5,g0)
    c: Equal(g0, g1-g5) x5
    c: PointOnObject(g0,g6)
    c: PointOnObject(g1,g6)
    c: PointOnObject(g2,g6)
    c: PointOnObject(g3,g6)
    c: PointOnObject(g4,g6)
    c: PointOnObject(g5,g6)
    c: Coincident(g6,g-1)
    c: PointOnObject(g0,g-2)
    c: DistanceX(g1,g0) = 2.55
FEATURE [PartDesign::Pocket] Pocket509  label="M3x20 Wrench044"
  BaseFeature = -> Pad564
  Length = 1.3
  Length2 = 100
  Profile = -> Sketch1505
  Type = 0
FEATURE [PartDesign::Chamfer] Chamfer291  label="M3x20 Smooth052"
  Base = -> Pocket509 [Face11,Edge2,Edge24,Edge3]
  BaseFeature = -> Pocket509
  Size = 0.2
FEATURE [PartDesign::Body] Body365  label="M3x076"
  Group = -> [Sketch1508,Pad562,Sketch1200,Pad564,Sketch1505,Pocket509,Chamfer291]
  Origin = -> Origin513
  Placement = pos=(11.3,-65.6,176.35) rot=(0,-1,0;1.5708rad)
  Tip = -> Chamfer291
FEATURE [Sketcher::SketchObject] Sketch1509
  MapMode = 5
  Placement = pos=(0,0,0) rot=(1,0,0;3.14159rad)
  Support = -> [Pad552]
  sketch-geometry (7):
    g0: LineSegment StartX=1.275 StartY=0.736122 StartZ=0 EndX=0 EndY=1.47224 EndZ=0
    g1: LineSegment StartX=0 StartY=1.47224 StartZ=0 EndX=-1.275 EndY=0.736122 EndZ=0
    g2: LineSegment StartX=-1.275 StartY=0.736122 StartZ=0 EndX=-1.275 EndY=-0.736122 EndZ=0
    g3: LineSegment StartX=-1.275 StartY=-0.736122 StartZ=0 EndX=1.34766e-11 EndY=-1.47224 EndZ=0
    g4: LineSegment StartX=1.34766e-11 StartY=-1.47224 StartZ=0 EndX=1.275 EndY=-0.736122 EndZ=0
    g5: LineSegment StartX=1.275 StartY=-0.736122 StartZ=0 EndX=1.275 EndY=0.736122 EndZ=0
    g6: Circle [constr] CenterX=0 CenterY=0 CenterZ=0 NormalX=0 NormalY=0 NormalZ=1 AngleXU=0 Radius=1.47224
  constraints (16):
    c: Coincident(g0,g1)
    c: Coincident(g1,g2)
    c: Coincident(g2,g3)
    c: Coincident(g3,g4)
    c: Coincident(g4,g5)
    c: Coincident(g5,g0)
    c: Equal(g0, g1-g5) x5
    c: PointOnObject(g0,g6)
    c: PointOnObject(g1,g6)
    c: PointOnObject(g2,g6)
    c: PointOnObject(g3,g6)
    c: PointOnObject(g4,g6)
    c: PointOnObject(g5,g6)
    c: Coincident(g6,g-1)
    c: PointOnObject(g0,g-2)
    c: DistanceX(g1,g0) = 2.55
FEATURE [PartDesign::Pocket] Pocket562  label="M3x20 Wrench055"
  BaseFeature = -> Pad552
  Length = 1.3
  Length2 = 100
  Profile = -> Sketch1509
  Type = 0
FEATURE [PartDesign::Chamfer] Chamfer226  label="M3x20 Smooth040"
  Base = -> Pocket562 [Face11,Edge2,Edge24,Edge3]
  BaseFeature = -> Pocket562
  Size = 0.2
FEATURE [PartDesign::Body] Body355  label="M3x074"
  Group = -> [Sketch1235,Pad568,Sketch1478,Pad552,Sketch1509,Pocket562,Chamfer226]
  Origin = -> Origin509
  Placement = pos=(11.3,-55.6,176.35) rot=(0,-1,0;1.5708rad)
  Tip = -> Chamfer226
FEATURE [App::Part] Part130  label="Servo Scres002"
  Group = -> [Body366,Body360,Body365,Body355]
  Origin = -> Origin552
FEATURE [PartDesign::Body] Body398  label="brown wire011"
  Group = -> [Sketch1226,Pad549]
  Origin = -> Origin478
  Placement = pos=(0,25.15,0) rot=(0,0,1;0rad)
  Tip = -> Pad549
FEATURE [PartDesign::Body] Body399  label="orange wire011"
  Group = -> [Sketch1209,Pad638]
  Origin = -> Origin444
  Placement = pos=(0,25.15,0) rot=(0,0,1;0rad)
  Tip = -> Pad638
FEATURE [App::Part] Part124  label="Servo010"
  Group = -> [Body367,Body386,Body373,Body399,Body398]
  Origin = -> Origin437
  Placement = pos=(-21.1341,-60.6,200.491) rot=(0.57735,0.57735,0.57735;2.0944rad)
FEATURE [PartDesign::Body] Body400  label="M3x085"
  Group = -> [Sketch1213,Pad634,Sketch1189,Pad630,Sketch1201,Pocket558,Chamfer238,Sketch1187]
  Origin = -> Origin522
  Placement = pos=(-5.2,-40,200.6) rot=(-1,0,0;1.5708rad)
  Tip = -> Chamfer238
FEATURE [PartDesign::Body] Body401  label="M2x061"
  Group = -> [Sketch1483,Pad602,Sketch1489,Pad637,Sketch1500,Pocket539,Chamfer239]
  Origin = -> Origin562
  Tip = -> Chamfer239
FEATURE [App::Part] Part150  label="M048"
  Group = -> [Body401,Body397]
  Origin = -> Origin545
  Placement = pos=(9.1,5.25,80) rot=(0,1,0;3.14159rad)
FEATURE [PartDesign::Body] Body402  label="M2 Nut052"
  Group = -> [Sketch1244,Pad639,Sketch1499,Groove121,Chamfer221,Sketch1488,Sketch1495]
  Origin = -> Origin531
  Placement = pos=(0,0,2.75) rot=(0,0,1;0rad)
  Tip = -> Chamfer221
FEATURE [App::Part] Part148  label="M047"
  Group = -> [Body370,Body402]
  Origin = -> Origin530
  Placement = pos=(9.1,-5.25,80) rot=(0,1,0;3.14159rad)
FEATURE [App::Part] Part145  label="Screws010"
  Group = -> [Part146,Part147,Part139,Part148,Part150,Part157]
  Origin = -> Origin571
  Placement = pos=(0,0,-71) rot=(0,0,1;0rad)
FEATURE [PartDesign::Body] Body403  label="M3 Nut071"
  Group = -> [Sketch1375,Pad586,Sketch1378,Groove118,Chamfer254]
  Origin = -> Origin419
  Placement = pos=(-115.35,-9.3,62.1) rot=(0.57735,0.57735,-0.57735;2.0944rad)
  Tip = -> Chamfer254
FEATURE [App::Part] Part122  label="Shell Nuts002"
  Group = -> [Body308,Body320,Body403,Body337]
  Origin = -> Origin462
FEATURE [PartDesign::Body] Body404  label="M2 Nut053"
  Group = -> [Sketch1503,Pad628,Sketch1184,Groove126,Chamfer228,Sketch1178,Sketch1180]
  Origin = -> Origin512
  Placement = pos=(-19.5,10,15) rot=(0.57735,0.57735,-0.57735;4.18879rad)
  Tip = -> Chamfer228
FEATURE [App::Part] Part152  label="SHOULDER PIN002"
  Group = -> [Body404,Body353,Body354]
  Origin = -> Origin416
  Placement = pos=(-3.6e-15,0,30) rot=(0,1,0;3.14159rad)
FEATURE [PartDesign::Body] Body405  label="Shoulder_Joint_Servomount002"
  Group = -> [Sketch1239,Pad626,Pad613,Sketch1252,Pocket544,Sketch1246,Pocket538,Sketch1421,Pocket533,Sketch1249,Pocket551,Sketch1432,Pocket552,Sketch1247,Pocket547,Sketch1261,Pocket555,Sketch1245,Pocket563,Sketch1430,Pocket545,Fillet187,Fillet152]
  Origin = -> Origin443
  Tip = -> Fillet152
FEATURE [Part::Mirroring] Part__Mirroring001  label="Shoulder_Joint_Servomount (Mirror #1)001"
  Base = (0,0,0)
  Normal = (0,0,1)
  Placement = pos=(0,0,0) rot=(0,1,0;3.14159rad)
  Source = -> Body405
FEATURE [PartDesign::Body] Body406  label="M3x086"
  Group = -> [Sketch1192,Pad615,Sketch1182,Pad611,Sketch1186,Pocket549,Chamfer240]
  Origin = -> Origin506
  Placement = pos=(-14.15,-14.15,-6) rot=(0,0,1;0rad)
  Tip = -> Chamfer240
FEATURE [App::Part] Part149  label="Shouldercap Screws002"
  Group = -> [Body378,Body376,Body375,Body406]
  Origin = -> Origin523
FEATURE [PartDesign::Body] Body407  label="M3x087"
  Group = -> [Sketch1321,Pad556,Sketch1297,Pad537,Sketch1320,Pocket500,Chamfer265]
  Origin = -> Origin496
  Placement = pos=(-114.75,-30,41) rot=(-1,0,0;1.5708rad)
  Tip = -> Chamfer265
FEATURE [App::Part] Part123  label="m3x20 screws002"
  Group = -> [Body316,Body385,Body377,Body407]
  Origin = -> Origin570
  Placement = pos=(-21.55,-12.1,-20.7) rot=(-0.707107,0,0.707107;3.14159rad)
FEATURE [PartDesign::Body] Body408  label="Limb_Bottom_Shell002"
  Group = -> [Sketch1305,Pad477,Pocket433,Pocket449,Sketch1439,SubtractivePipe013,Fillet179,Sketch1453,Pocket447,Sketch1282,Pocket440,Sketch1436,Pocket434,Pad473,Fillet176,Sketch1434,Pocket426,Fillet159,Sketch1333,Pocket446,Sketch1296,Pocket439,Sketch1443,Pocket442,Sketch1286,Pocket429,Sketch1330,Pocket424,Sketch1445,Pocket506,Sketch1442,Pocket427,Sketch1279,Pocket428,Sketch1292,Pocket493,Sketch1290,Pocket453,+5 more]
  Origin = -> Origin491
  Placement = pos=(-144.05,-29.45,42.05) rot=(0,0,1;0rad)
  Tip = -> Fillet183
FEATURE [Part::Mirroring] Part__Mirroring006  label="Limb_Bottom_Shell001 (Mirror #7)"
  Base = (0,0,0)
  Normal = (0,0,1)
  Placement = pos=(0,-1.9,0) rot=(1,0,0;3.14159rad)
  Source = -> Body408
FEATURE [App::Part] Part119  label="FR Upper Leg"
  Group = -> [Part153,Part137,Body295,Body408,Part122,Part126,Part133,Part115,Part117,Part135,Body384,Part121,Part__Mirroring005,Part__Mirroring006]
  Origin = -> Origin414
  Placement = pos=(55.5497,1.3,169.885) rot=(0,1,0;5.75959rad)
FEATURE [PartDesign::Body] Body409  label="M3 Nut072"
  Group = -> [Sketch1174,Pad650,Sketch1176,Groove128,Chamfer232]
  Origin = -> Origin538
  Placement = pos=(14.15,-14.15,3.5) rot=(0,0,1;0.261799rad)
  Tip = -> Chamfer232
FEATURE [App::Part] Part128  label="Shouldercap Nuts002"
  Group = -> [Body363,Body371,Body409,Body368]
  Origin = -> Origin542
FEATURE [PartDesign::Body] Body410  label="M3 Nut073"
  Group = -> [Sketch1211,Pad643,Sketch1224,Groove130,Chamfer234]
  Origin = -> Origin451
  Placement = pos=(5e-14,-55.6,224.85) rot=(0.57735,-0.57735,0.57735;4.18879rad)
  Tip = -> Chamfer234
FEATURE [App::Part] Part129  label="FL Shoulder Joint Servo002"
  Group = -> [Part124,Body381,Body380,Body364,Body410,Part130,Part120]
  Origin = -> Origin418
  Placement = pos=(-5.4,-200.45,75.6) rot=(0,0.707107,0.707107;3.14159rad)
FEATURE [PartDesign::Body] Body411  label="Futuba FSH6B007"
  Group = -> [Sketch1256,Pad597,Sketch1418,Pocket541,Sketch1248,Pocket531,Sketch1243,Pocket530,Sketch1230,Pad621,Fillet158,Sketch1266]
  Origin = -> Origin529
  Tip = -> Fillet158
FEATURE [App::Part] Part144  label="Servphorn002"
  Group = -> [Body411]
  Origin = -> Origin528
  Placement = pos=(0,0,3.45) rot=(0,0,1;0rad)
FEATURE [App::Part] Part155  label="Shoulderjoint CAP002"
  Group = -> [Part145,Part144,Body383]
  Origin = -> Origin427
  Placement = pos=(0,0,-12) rot=(0,0,1;0rad)
FEATURE [App::Part] Part154  label="RL Shoulder Joint001"
  Group = -> [Body405,Part155,Part152,Part128,Part149,Body400,Part__Mirroring001,Part129]
  Origin = -> Origin548
  Placement = pos=(-5.2,-45.6,200.6) rot=(1,0,0;1.5708rad)
FEATURE [App::Part] Part158  label="Ball Bearing Pin006"
  Group = -> [Body328,Body302,Body347]
  Origin = -> Origin573
  Placement = pos=(-247.6,-327.45,0) rot=(0,0,1;3.14159rad)
FEATURE [App::Part] Part132  label="Lower Leg Counterpiece and Ball Bearing Pin002"
  Group = -> [Body296,Body330,Body344,Body329,Body346,Part__Mirroring002,Part158]
  Origin = -> Origin467
  Placement = pos=(49.45,155,49.5) rot=(0,0,1;0rad)
FEATURE [App::Part] Part131  label="FR Lower Leg"
  Group = -> [Part114,Part125,Part156,Part132,Part123,Part116,Part118]
  Origin = -> Origin476
  Placement = pos=(-0.0178536,-0.55,0.205627) rot=(0,0,1;0rad)
FEATURE [App::Part] Part159
  Group = -> [Part154]
  Origin = -> Origin574
  Placement = pos=(-10.1,1.2e-15,0) rot=(0,0,1;3.14159rad)
FEATURE [App::Part] Part151  label="FR Leg"
  Group = -> [Part131,Part119,Part159]
  Origin = -> Origin555
  Placement = pos=(-0.1,-199.3,-0.2) rot=(0,0,1;0rad)
FEATURE [Sketcher::SketchObject] Sketch1528
  MapMode = 5
  Support = -> [XY_Plane590]
  sketch-geometry (4):
    g0: LineSegment StartX=0 StartY=0 StartZ=0 EndX=56.5 EndY=0 EndZ=0
    g1: LineSegment StartX=56.5 StartY=0 StartZ=0 EndX=56.5 EndY=-22 EndZ=0
    g2: LineSegment StartX=56.5 StartY=-22 StartZ=0 EndX=0 EndY=-22 EndZ=0
    g3: LineSegment StartX=0 StartY=-22 StartZ=0 EndX=0 EndY=0 EndZ=0
  constraints (11):
    c: Coincident(g0,g1)
    c: Coincident(g1,g2)
    c: Coincident(g2,g3)
    c: Coincident(g3,g0)
    c: Horizontal(g0)
    c: Horizontal(g2)
    c: Vertical(g1)
    c: Vertical(g3)
    c: Coincident(g0,g-1)
    c: DistanceX(g2,g2) = 56.5
    c: DistanceY(g3,g3) = 22
FEATURE [Sketcher::SketchObject] Sketch1530
  MapMode = 5
  Support = -> [XY_Plane594]
  sketch-geometry (8):
    g0: LineSegment StartX=0 StartY=3.17543 StartZ=0 EndX=-2.75 EndY=1.58771 EndZ=0
    g1: LineSegment StartX=-2.75 StartY=1.58771 StartZ=0 EndX=-2.75 EndY=-1.58771 EndZ=0
    g2: LineSegment StartX=-2.75 StartY=-1.58771 StartZ=0 EndX=0 EndY=-3.17543 EndZ=0
    g3: LineSegment StartX=0 StartY=-3.17543 StartZ=0 EndX=2.75 EndY=-1.58771 EndZ=0
    g4: LineSegment StartX=2.75 StartY=-1.58771 StartZ=0 EndX=2.75 EndY=1.58771 EndZ=0
    g5: LineSegment StartX=2.75 StartY=1.58771 StartZ=0 EndX=0 EndY=3.17543 EndZ=0
    g6: Circle [constr] CenterX=0 CenterY=0 CenterZ=0 NormalX=0 NormalY=0 NormalZ=1 AngleXU=0 Radius=3.17543
    g7: Circle CenterX=0 CenterY=0 CenterZ=0 NormalX=0 NormalY=0 NormalZ=1 AngleXU=0 Radius=1.5
  constraints (18):
    c: Coincident(g0,g1)
    c: Coincident(g1,g2)
    c: Coincident(g2,g3)
    c: Coincident(g3,g4)
    c: Coincident(g4,g5)
    c: Coincident(g5,g0)
    c: Equal(g0, g1-g5) x5
    c: PointOnObject(g0,g6)
    c: PointOnObject(g1,g6)
    c: PointOnObject(g2,g6)
    c: PointOnObject(g3,g6)
    c: PointOnObject(g4,g6)
    c: PointOnObject(g5,g6)
    c: Coincident(g6,g-1)
    c: PointOnObject(g5,g-2)
    c: DistanceX(g0,g4) = 5.5
    c: Coincident(g7,g-1)
    c: Radius(g7) = 1.5
FEATURE [Sketcher::SketchObject] Sketch1534
  MapMode = 5
  Support = -> [XY_Plane604]
  sketch-geometry (8):
    g0: LineSegment StartX=0 StartY=3.17543 StartZ=0 EndX=-2.75 EndY=1.58771 EndZ=0
    g1: LineSegment StartX=-2.75 StartY=1.58771 StartZ=0 EndX=-2.75 EndY=-1.58771 EndZ=0
    g2: LineSegment StartX=-2.75 StartY=-1.58771 StartZ=0 EndX=0 EndY=-3.17543 EndZ=0
    g3: LineSegment StartX=0 StartY=-3.17543 StartZ=0 EndX=2.75 EndY=-1.58771 EndZ=0
    g4: LineSegment StartX=2.75 StartY=-1.58771 StartZ=0 EndX=2.75 EndY=1.58771 EndZ=0
    g5: LineSegment StartX=2.75 StartY=1.58771 StartZ=0 EndX=0 EndY=3.17543 EndZ=0
    g6: Circle [constr] CenterX=0 CenterY=0 CenterZ=0 NormalX=0 NormalY=0 NormalZ=1 AngleXU=0 Radius=3.17543
    g7: Circle CenterX=0 CenterY=0 CenterZ=0 NormalX=0 NormalY=0 NormalZ=1 AngleXU=0 Radius=1.5
  constraints (18):
    c: Coincident(g0,g1)
    c: Coincident(g1,g2)
    c: Coincident(g2,g3)
    c: Coincident(g3,g4)
    c: Coincident(g4,g5)
    c: Coincident(g5,g0)
    c: Equal(g0, g1-g5) x5
    c: PointOnObject(g0,g6)
    c: PointOnObject(g1,g6)
    c: PointOnObject(g2,g6)
    c: PointOnObject(g3,g6)
    c: PointOnObject(g4,g6)
    c: PointOnObject(g5,g6)
    c: Coincident(g6,g-1)
    c: PointOnObject(g5,g-2)
    c: DistanceX(g0,g4) = 5.5
    c: Coincident(g7,g-1)
    c: Radius(g7) = 1.5
FEATURE [Sketcher::SketchObject] Sketch1537
  MapMode = 5
  Support = -> [XY_Plane582]
  sketch-geometry (8):
    g0: LineSegment StartX=-20 StartY=14 StartZ=0 EndX=20 EndY=14 EndZ=0
    g1: LineSegment StartX=20 StartY=14 StartZ=0 EndX=20 EndY=19 EndZ=0
    g2: LineSegment StartX=20 StartY=19 StartZ=0 EndX=-20 EndY=19 EndZ=0
    g3: LineSegment StartX=-20 StartY=19 StartZ=0 EndX=-20 EndY=14 EndZ=0
    g4: LineSegment StartX=-20 StartY=-19 StartZ=0 EndX=20 EndY=-19 EndZ=0
    g5: LineSegment StartX=20 StartY=-19 StartZ=0 EndX=20 EndY=-14 EndZ=0
    g6: LineSegment StartX=20 StartY=-14 StartZ=0 EndX=-20 EndY=-14 EndZ=0
    g7: LineSegment StartX=-20 StartY=-14 StartZ=0 EndX=-20 EndY=-19 EndZ=0
  constraints (22):
    c: Coincident(g0,g1)
    c: Coincident(g1,g2)
    c: Coincident(g2,g3)
    c: Coincident(g3,g0)
    c: Horizontal(g0)
    c: Vertical(g1)
    c: Vertical(g3)
    c: Coincident(g4,g5)
    c: Coincident(g5,g6)
    c: Coincident(g6,g7)
    c: Coincident(g7,g4)
    c: Horizontal(g4)
    c: Horizontal(g6)
    c: Vertical(g5)
    c: Vertical(g7)
    c: Equal(g1,g5)
    c: Equal(g6,g2)
    c: Symmetric(g1,g2,g-2)
    c: Symmetric(g1,g4,g-1)
    c: DistanceY(g1,g1) = 5
    c: DistanceY(g5,g0) = 28
    c: DistanceX(g2,g2) = 40
FEATURE [Sketcher::SketchObject] Sketch1539
  MapMode = 5
  Support = -> [XY_Plane592]
  sketch-geometry (8):
    g0: LineSegment StartX=0 StartY=3.17543 StartZ=0 EndX=-2.75 EndY=1.58771 EndZ=0
    g1: LineSegment StartX=-2.75 StartY=1.58771 StartZ=0 EndX=-2.75 EndY=-1.58771 EndZ=0
    g2: LineSegment StartX=-2.75 StartY=-1.58771 StartZ=0 EndX=0 EndY=-3.17543 EndZ=0
    g3: LineSegment StartX=0 StartY=-3.17543 StartZ=0 EndX=2.75 EndY=-1.58771 EndZ=0
    g4: LineSegment StartX=2.75 StartY=-1.58771 StartZ=0 EndX=2.75 EndY=1.58771 EndZ=0
    g5: LineSegment StartX=2.75 StartY=1.58771 StartZ=0 EndX=0 EndY=3.17543 EndZ=0
    g6: Circle [constr] CenterX=0 CenterY=0 CenterZ=0 NormalX=0 NormalY=0 NormalZ=1 AngleXU=0 Radius=3.17543
    g7: Circle CenterX=0 CenterY=0 CenterZ=0 NormalX=0 NormalY=0 NormalZ=1 AngleXU=0 Radius=1.5
  constraints (18):
    c: Coincident(g0,g1)
    c: Coincident(g1,g2)
    c: Coincident(g2,g3)
    c: Coincident(g3,g4)
    c: Coincident(g4,g5)
    c: Coincident(g5,g0)
    c: Equal(g0, g1-g5) x5
    c: PointOnObject(g0,g6)
    c: PointOnObject(g1,g6)
    c: PointOnObject(g2,g6)
    c: PointOnObject(g3,g6)
    c: PointOnObject(g4,g6)
    c: PointOnObject(g5,g6)
    c: Coincident(g6,g-1)
    c: PointOnObject(g5,g-2)
    c: DistanceX(g0,g4) = 5.5
    c: Coincident(g7,g-1)
    c: Radius(g7) = 1.5
FEATURE [Sketcher::SketchObject] Sketch1543
  MapMode = 5
  Support = -> [XY_Plane585]
  sketch-geometry (8):
    g0: LineSegment StartX=0 StartY=2.3094 StartZ=0 EndX=-2 EndY=1.1547 EndZ=0
    g1: LineSegment StartX=-2 StartY=1.1547 StartZ=0 EndX=-2 EndY=-1.1547 EndZ=0
    g2: LineSegment StartX=-2 StartY=-1.1547 StartZ=0 EndX=-2e-16 EndY=-2.3094 EndZ=0
    g3: LineSegment StartX=-2e-16 StartY=-2.3094 StartZ=0 EndX=2 EndY=-1.1547 EndZ=0
    g4: LineSegment StartX=2 StartY=-1.1547 StartZ=0 EndX=2 EndY=1.1547 EndZ=0
    g5: LineSegment StartX=2 StartY=1.1547 StartZ=0 EndX=0 EndY=2.3094 EndZ=0
    g6: Circle [constr] CenterX=0 CenterY=0 CenterZ=0 NormalX=0 NormalY=0 NormalZ=1 AngleXU=0 Radius=2.3094
    g7: Circle CenterX=0 CenterY=0 CenterZ=0 NormalX=0 NormalY=0 NormalZ=1 AngleXU=0 Radius=1
  constraints (18):
    c: Coincident(g0,g1)
    c: Coincident(g1,g2)
    c: Coincident(g2,g3)
    c: Coincident(g3,g4)
    c: Coincident(g4,g5)
    c: Coincident(g5,g0)
    c: Equal(g0, g1-g5) x5
    c: PointOnObject(g0,g6)
    c: PointOnObject(g1,g6)
    c: PointOnObject(g2,g6)
    c: PointOnObject(g3,g6)
    c: PointOnObject(g4,g6)
    c: PointOnObject(g5,g6)
    c: Coincident(g6,g-1)
    c: PointOnObject(g5,g-2)
    c: DistanceX(g0,g4) = 4
    c: Coincident(g7,g-1)
    c: Radius(g7) = 1
FEATURE [Sketcher::SketchObject] Sketch1546
  MapMode = 5
  Placement = pos=(0,0,0) rot=(0.57735,0.57735,0.57735;2.0944rad)
  Support = -> [YZ_Plane599]
  sketch-geometry (4):
    g0: LineSegment StartX=35.5 StartY=12.9 StartZ=0 EndX=38.5 EndY=12.9 EndZ=0
    g1: LineSegment StartX=38.5 StartY=12.9 StartZ=0 EndX=38.5 EndY=7.1 EndZ=0
    g2: LineSegment StartX=38.5 StartY=7.1 StartZ=0 EndX=35.5 EndY=7.1 EndZ=0
    g3: LineSegment StartX=35.5 StartY=7.1 StartZ=0 EndX=35.5 EndY=12.9 EndZ=0
  constraints (12):
    c: Coincident(g0,g1)
    c: Coincident(g1,g2)
    c: Coincident(g2,g3)
    c: Coincident(g3,g0)
    c: Horizontal(g0)
    c: Horizontal(g2)
    c: Vertical(g1)
    c: Vertical(g3)
    c: DistanceY(g-1,g1) = 7.1
    c: DistanceY(g3,g3) = 5.8
    c: DistanceX(g0,g0) = 3
    c: DistanceX(g-1,g1) = 38.5
FEATURE [Sketcher::SketchObject] Sketch1552
  MapMode = 5
  Placement = pos=(0,0,0) rot=(1,0,0;1.5708rad)
  Support = -> [XZ_Plane660]
  sketch-geometry (1):
    g0: Circle CenterX=-1.55 CenterY=4 CenterZ=0 NormalX=0 NormalY=0 NormalZ=1 AngleXU=0 Radius=0.75
  constraints (3):
    c: Radius(g0) = 0.75
    c: DistanceY(g-1,g0) = 4
    c: DistanceX(g0,g-1) = 1.55
FEATURE [Sketcher::SketchObject] Sketch1556
  MapMode = 5
  Support = -> [XY_Plane683]
  sketch-geometry (9):
    g0: ArcOfCircle CenterX=0 CenterY=0 CenterZ=0 NormalX=0 NormalY=0 NormalZ=1 AngleXU=0 Radius=16.5 StartAngle=3.66519 EndAngle=6.80678
    g1: LineSegment StartX=-14.2894 StartY=-8.25 StartZ=0 EndX=-27.2211 EndY=14.1484 EndZ=0
    g2: LineSegment StartX=1.3577 StartY=30.6484 StartZ=0 EndX=14.2894 EndY=8.25 EndZ=0
    g3: LineSegment [constr] StartX=-27.2211 StartY=14.1484 StartZ=0 EndX=1.3577 EndY=30.6484 EndZ=0
    g4: ArcOfCircle CenterX=-28.6962 CenterY=13.2968 CenterZ=0 NormalX=0 NormalY=0 NormalZ=1 AngleXU=0 Radius=1.70319 StartAngle=0.523599 EndAngle=1.5708
    g5: ArcOfCircle CenterX=-23.5 CenterY=16.2968 CenterZ=0 NormalX=0 NormalY=0 NormalZ=1 AngleXU=0 Radius=28.7032 StartAngle=0.523599 EndAngle=1.5708
    g6: LineSegment StartX=-28.6962 StartY=15 StartZ=0 EndX=-40 EndY=15 EndZ=0
    g7: LineSegment StartX=-40 StartY=15 StartZ=0 EndX=-40 EndY=45 EndZ=0
    g8: LineSegment StartX=-40 StartY=45 StartZ=0 EndX=-23.5 EndY=45 EndZ=0
  constraints (22):
    c: Coincident(g0,g-1)
    c: Tangent(g0,g1) = 1.5708
    c: Coincident(g3,g2) = -1.5708
    c: Parallel(g2,g1)
    c: Radius(g0) = 16.5
    c: Tangent(g2,g0) = 1.5708
    c: Coincident(g3,g1)
    c: Perpendicular(g1,g3)
    c: Tangent(g5,g2) = 1.5708
    c: Tangent(g4,g1) = -1.5708
    c: Horizontal(g6)
    c: Coincident(g7,g6)
    c: Vertical(g7)
    c: Coincident(g8,g7)
    c: Horizontal(g8)
    c: Tangent(g6,g4) = -1.5708
    c: DistanceY(g7,g7) = 30
    c: DistanceX(g6,g0) = 40
    c: DistanceX(g8,g8) = 16.5
    c: Tangent(g8,g5) = 1.5708
    c: DistanceY(g0,g4) = 15
    c: Angle(g3) = 0.523599
FEATURE [Sketcher::SketchObject] Sketch1557
  MapMode = 5
  Support = -> [XY_Plane652]
  sketch-geometry (1):
    g0: Circle CenterX=0 CenterY=0 CenterZ=0 NormalX=0 NormalY=0 NormalZ=1 AngleXU=0 Radius=1.9
  constraints (2):
    c: Coincident(g0,g-1)
    c: Radius(g0) = 1.9
FEATURE [Sketcher::SketchObject] Sketch1558
  MapMode = 5
  Support = -> [XY_Plane679]
FEATURE [Sketcher::SketchObject] Sketch1559
  MapMode = 5
  Placement = pos=(0,0,0) rot=(1,0,0;1.5708rad)
  Support = -> [XZ_Plane581]
  sketch-geometry (1):
    g0: Circle CenterX=0 CenterY=4 CenterZ=0 NormalX=0 NormalY=0 NormalZ=1 AngleXU=0 Radius=0.75
  constraints (3):
    c: PointOnObject(g0,g-2)
    c: Radius(g0) = 0.75
    c: DistanceY(g-1,g0) = 4
FEATURE [Sketcher::SketchObject] Sketch1561
  MapMode = 5
  Support = -> [XY_Plane651]
FEATURE [Sketcher::SketchObject] Sketch1562
  MapMode = 5
  Support = -> [XY_Plane651]
FEATURE [Sketcher::SketchObject] Sketch1564
  MapMode = 5
  Support = -> [XY_Plane596]
  sketch-geometry (12):
    g0: LineSegment StartX=0 StartY=0 StartZ=0 EndX=0 EndY=57 EndZ=0
    g1: LineSegment StartX=0 StartY=57 StartZ=0 EndX=40 EndY=57 EndZ=0
    g2: ArcOfCircle CenterX=40 CenterY=44.5 CenterZ=0 NormalX=0 NormalY=0 NormalZ=1 AngleXU=0 Radius=12.5 StartAngle=0.643501 EndAngle=1.5708
    g3: ArcOfCircle CenterX=60 CenterY=59.5 CenterZ=0 NormalX=0 NormalY=0 NormalZ=1 AngleXU=0 Radius=12.5 StartAngle=3.78509 EndAngle=4.71239
    g4: LineSegment StartX=60 StartY=47 StartZ=0 EndX=120 EndY=47 EndZ=0
    g5: ArcOfCircle CenterX=120 CenterY=37 CenterZ=0 NormalX=0 NormalY=0 NormalZ=1 AngleXU=0 Radius=10 StartAngle=2e-16 EndAngle=1.5708
    g6: LineSegment StartX=130 StartY=37 StartZ=0 EndX=130 EndY=15 EndZ=0
    g7: ArcOfCircle CenterX=125 CenterY=15 CenterZ=0 NormalX=0 NormalY=0 NormalZ=1 AngleXU=0 Radius=5 StartAngle=4.71239 EndAngle=6.28319
    g8: LineSegment StartX=125 StartY=10 StartZ=0 EndX=60 EndY=10 EndZ=0
    g9: LineSegment StartX=40 StartY=0 StartZ=0 EndX=0 EndY=0 EndZ=0
    g10: ArcOfCircle CenterX=40 CenterY=12.5 CenterZ=0 NormalX=0 NormalY=0 NormalZ=1 AngleXU=0 Radius=12.5 StartAngle=4.71239 EndAngle=5.63968
    g11: ArcOfCircle CenterX=60 CenterY=-2.5 CenterZ=0 NormalX=0 NormalY=0 NormalZ=1 AngleXU=0 Radius=12.5 StartAngle=1.5708 EndAngle=2.49809
  constraints (31):
    c: Coincident(g-1,g0)
    c: PointOnObject(g0,g-2)
    c: Coincident(g0,g1)
    c: Horizontal(g1)
    c: Tangent(g1,g2) = 1.5708
    c: Tangent(g2,g3) = 1.5708
    c: Tangent(g3,g4) = -1.5708
    c: Tangent(g4,g5) = 1.5708
    c: Tangent(g5,g6) = 1.5708
    c: Tangent(g6,g7) = 1.5708
    c: Tangent(g7,g8) = 1.5708
    c: Coincident(g9,g0)
    c: Horizontal(g9)
    c: Horizontal(g4)
    c: Horizontal(g8)
    c: Vertical(g6)
    c: Tangent(g11,g8) = -1.5708
    c: Tangent(g11,g10) = 1.5708
    c: Radius(g7) = 5
    c: Radius(g5) = 10
    c: DistanceX(g1,g1) = 40
    c: DistanceX(g0,g6) = 130
    c: DistanceX(g1,g3) = 20
    c: Tangent(g10,g9) = 1.5708
    c: DistanceX(g9,g8) = 20
    c: DistanceX(g9,g9) = 40
    c: DistanceY(g0,g0) = 57
    c: DistanceY(g9,g8) = 10
    c: DistanceY(g3,g1) = 10
    c: DistanceX(g10,g8) = 10
    c: DistanceX(g2,g3) = 10
FEATURE [Sketcher::SketchObject] Sketch1566
  MapMode = 5
  Support = -> [XY_Plane583]
  sketch-geometry (8):
    g0: LineSegment StartX=0 StartY=3.17543 StartZ=0 EndX=-2.75 EndY=1.58771 EndZ=0
    g1: LineSegment StartX=-2.75 StartY=1.58771 StartZ=0 EndX=-2.75 EndY=-1.58771 EndZ=0
    g2: LineSegment StartX=-2.75 StartY=-1.58771 StartZ=0 EndX=0 EndY=-3.17543 EndZ=0
    g3: LineSegment StartX=0 StartY=-3.17543 StartZ=0 EndX=2.75 EndY=-1.58771 EndZ=0
    g4: LineSegment StartX=2.75 StartY=-1.58771 StartZ=0 EndX=2.75 EndY=1.58771 EndZ=0
    g5: LineSegment StartX=2.75 StartY=1.58771 StartZ=0 EndX=0 EndY=3.17543 EndZ=0
    g6: Circle [constr] CenterX=0 CenterY=0 CenterZ=0 NormalX=0 NormalY=0 NormalZ=1 AngleXU=0 Radius=3.17543
    g7: Circle CenterX=0 CenterY=0 CenterZ=0 NormalX=0 NormalY=0 NormalZ=1 AngleXU=0 Radius=1.5
  constraints (18):
    c: Coincident(g0,g1)
    c: Coincident(g1,g2)
    c: Coincident(g2,g3)
    c: Coincident(g3,g4)
    c: Coincident(g4,g5)
    c: Coincident(g5,g0)
    c: Equal(g0, g1-g5) x5
    c: PointOnObject(g0,g6)
    c: PointOnObject(g1,g6)
    c: PointOnObject(g2,g6)
    c: PointOnObject(g3,g6)
    c: PointOnObject(g4,g6)
    c: PointOnObject(g5,g6)
    c: Coincident(g6,g-1)
    c: PointOnObject(g5,g-2)
    c: DistanceX(g0,g4) = 5.5
    c: Coincident(g7,g-1)
    c: Radius(g7) = 1.5
FEATURE [Sketcher::SketchObject] Sketch1569
  MapMode = 5
  Placement = pos=(0,0,0) rot=(1,0,0;1.5708rad)
  Support = -> [XZ_Plane683]
  sketch-geometry (1):
    g0: Circle CenterX=1.55 CenterY=4 CenterZ=0 NormalX=0 NormalY=0 NormalZ=1 AngleXU=0 Radius=0.75
  constraints (3):
    c: Radius(g0) = 0.75
    c: DistanceY(g-1,g0) = 4
    c: DistanceX(g-1,g0) = 1.55
FEATURE [Sketcher::SketchObject] Sketch1570
  MapMode = 5
  Support = -> [XY_Plane579]
  sketch-geometry (2):
    g0: Circle CenterX=0 CenterY=0 CenterZ=0 NormalX=0 NormalY=0 NormalZ=1 AngleXU=0 Radius=2.5
    g1: Circle CenterX=0 CenterY=0 CenterZ=0 NormalX=0 NormalY=0 NormalZ=1 AngleXU=0 Radius=1
  constraints (4):
    c: Coincident(g0,g-1)
    c: Coincident(g1,g0)
    c: Radius(g0) = 2.5
    c: Radius(g1) = 1
FEATURE [Sketcher::SketchObject] Sketch1572
  MapMode = 5
  Support = -> [XY_Plane589]
  sketch-geometry (1):
    g0: Circle CenterX=0 CenterY=0 CenterZ=0 NormalX=0 NormalY=0 NormalZ=1 AngleXU=0 Radius=2.75
  constraints (2):
    c: Coincident(g0,g-1)
    c: Radius(g0) = 2.75
FEATURE [Sketcher::SketchObject] Sketch1574
  MapMode = 5
  Support = -> [XY_Plane685]
  sketch-geometry (1):
    g0: Circle CenterX=0 CenterY=0 CenterZ=0 NormalX=0 NormalY=0 NormalZ=1 AngleXU=0 Radius=2.75
  constraints (2):
    c: Coincident(g0,g-1)
    c: Radius(g0) = 2.75
FEATURE [Sketcher::SketchObject] Sketch1575
  MapMode = 5
  Support = -> [XY_Plane689]
  sketch-geometry (1):
    g0: Circle CenterX=0 CenterY=10.15 CenterZ=0 NormalX=0 NormalY=0 NormalZ=1 AngleXU=0 Radius=3
  constraints (3):
    c: PointOnObject(g0,g-2)
    c: DistanceY(g-1,g0) = 10.15
    c: Radius(g0) = 3
FEATURE [Sketcher::SketchObject] Sketch1577
  MapMode = 5
  Support = -> [XY_Plane601]
  sketch-geometry (1):
    g0: Circle CenterX=0 CenterY=0 CenterZ=0 NormalX=0 NormalY=0 NormalZ=1 AngleXU=0 Radius=2.75
  constraints (2):
    c: Coincident(g0,g-1)
    c: Radius(g0) = 2.75
FEATURE [Sketcher::SketchObject] Sketch1585
  MapMode = 5
  Support = -> [XY_Plane591]
  sketch-geometry (9):
    g0: LineSegment StartX=-2.8e-15 StartY=0 StartZ=0 EndX=56.5 EndY=0 EndZ=0
    g1: LineSegment StartX=56.5 StartY=0 StartZ=0 EndX=56.5 EndY=25 EndZ=0
    g2: LineSegment StartX=51.5 StartY=30 StartZ=0 EndX=-80 EndY=30 EndZ=0
    g3: ArcOfCircle CenterX=-80 CenterY=15 CenterZ=0 NormalX=0 NormalY=0 NormalZ=1 AngleXU=0 Radius=15 StartAngle=1.5708 EndAngle=5.50197
    g4: ArcOfCircle CenterX=-50 CenterY=-14.75 CenterZ=0 NormalX=0 NormalY=0 NormalZ=1 AngleXU=0 Radius=27.25 StartAngle=1.5708 EndAngle=2.36038
    g5: ArcOfCircle CenterX=-30 CenterY=-14.75 CenterZ=0 NormalX=0 NormalY=0 NormalZ=1 AngleXU=0 Radius=27.25 StartAngle=0.781214 EndAngle=1.5708
    g6: ArcOfCircle CenterX=0 CenterY=15 CenterZ=0 NormalX=0 NormalY=0 NormalZ=1 AngleXU=0 Radius=15 StartAngle=3.92281 EndAngle=4.71239
    g7: LineSegment StartX=-50 StartY=12.5 StartZ=0 EndX=-30 EndY=12.5 EndZ=0
    g8: ArcOfCircle CenterX=51.5 CenterY=25 CenterZ=0 NormalX=0 NormalY=0 NormalZ=1 AngleXU=0 Radius=5 StartAngle=3e-16 EndAngle=1.5708
  constraints (23):
    c: Coincident(g0,g1)
    c: Horizontal(g0)
    c: Horizontal(g2)
    c: Vertical(g1)
    c: DistanceX(g0,g0) = 56.5
    c: Horizontal(g7)
    c: Radius(g3) = 15
    c: Tangent(g7,g5) = 1.5708
    c: Tangent(g4,g3) = 1.5708
    c: Tangent(g3,g2) = -1.5708
    c: Tangent(g7,g4) = 1.5708
    c: Tangent(g6,g5) = 1.5708
    c: Tangent(g6,g0) = -1.5708
    c: Equal(g3,g6)
    c: Equal(g4,g5)
    c: DistanceY(g0,g5) = 12.5
    c: DistanceX(g2,g0) = 80
    c: DistanceX(g4,g5) = 20
    c: Tangent(g3,g-1)
    c: Tangent(g2,g8) = -1.5708
    c: Tangent(g1,g8) = -1.5708
    c: Radius(g8) = 5
    c: Coincident(g0,g-1)
FEATURE [Sketcher::SketchObject] Sketch1597
  MapMode = 5
  Support = -> [XY_Plane586]
  sketch-geometry (4):
    g0: LineSegment StartX=-10 StartY=20.15 StartZ=0 EndX=10 EndY=20.15 EndZ=0
    g1: LineSegment StartX=10 StartY=20.15 StartZ=0 EndX=10 EndY=-20.15 EndZ=0
    g2: LineSegment StartX=10 StartY=-20.15 StartZ=0 EndX=-10 EndY=-20.15 EndZ=0
    g3: LineSegment StartX=-10 StartY=-20.15 StartZ=0 EndX=-10 EndY=20.15 EndZ=0
  constraints (10):
    c: Coincident(g0,g1)
    c: Coincident(g1,g2)
    c: Coincident(g2,g3)
    c: Coincident(g3,g0)
    c: Horizontal(g2)
    c: Vertical(g3)
    c: DistanceX(g0,g0) = 20
    c: DistanceY(g1,g1) = 40.3
    c: Symmetric(g0,g1,g-1)
    c: Symmetric(g0,g0,g-2)
FEATURE [Sketcher::SketchObject] Sketch1599
  MapMode = 5
  Placement = pos=(0,0,0) rot=(1,0,0;1.5708rad)
  Support = -> [XZ_Plane591]
  sketch-geometry (2):
    g0: ArcOfCircle CenterX=0 CenterY=0 CenterZ=0 NormalX=0 NormalY=0 NormalZ=1 AngleXU=0 Radius=20 StartAngle=-1.8e-15 EndAngle=3.14159
    g1: LineSegment StartX=-20 StartY=-1.38798e-11 StartZ=0 EndX=20 EndY=-3.55e-14 EndZ=0
  constraints (6):
    c: Coincident(g0,g-1)
    c: PointOnObject(g0,g-1)
    c: PointOnObject(g0,g-1)
    c: Coincident(g1,g0)
    c: Coincident(g1,g0)
    c: Radius(g0) = 20
FEATURE [Sketcher::SketchObject] Sketch1601
  MapMode = 5
  Placement = pos=(0,0,0) rot=(1,0,0;1.5708rad)
  Support = -> [XZ_Plane591]
  sketch-geometry (6):
    g0: LineSegment StartX=-15 StartY=0 StartZ=0 EndX=-25 EndY=7.5 EndZ=0
    g1: LineSegment StartX=-25 StartY=7.5 StartZ=0 EndX=-25 EndY=-7.5 EndZ=0
    g2: LineSegment StartX=-25 StartY=-7.5 StartZ=0 EndX=25 EndY=-7.5 EndZ=0
    g3: LineSegment StartX=25 StartY=-7.5 StartZ=0 EndX=25 EndY=7.5 EndZ=0
    g4: LineSegment StartX=25 StartY=7.5 StartZ=0 EndX=15 EndY=0 EndZ=0
    g5: LineSegment StartX=15 StartY=0 StartZ=0 EndX=-15 EndY=0 EndZ=0
  constraints (15):
    c: PointOnObject(g0,g-1)
    c: Coincident(g0,g1)
    c: Vertical(g1)
    c: Coincident(g1,g2)
    c: Horizontal(g2)
    c: Coincident(g2,g3)
    c: Coincident(g3,g4)
    c: Coincident(g4,g5)
    c: Coincident(g5,g0)
    c: DistanceX(g5,g5) = 30
    c: DistanceX(g4,g2) = 10
    c: Symmetric(g0,g4,g-2)
    c: Symmetric(g0,g3,g-2)
    c: DistanceY(g-1,g3) = 7.5
    c: Symmetric(g2,g3,g-1)
FEATURE [Sketcher::SketchObject] Sketch1602
  MapMode = 5
  Support = -> [XY_Plane576]
  sketch-geometry (8):
    g0: LineSegment StartX=0 StartY=3.17543 StartZ=0 EndX=-2.75 EndY=1.58771 EndZ=0
    g1: LineSegment StartX=-2.75 StartY=1.58771 StartZ=0 EndX=-2.75 EndY=-1.58771 EndZ=0
    g2: LineSegment StartX=-2.75 StartY=-1.58771 StartZ=0 EndX=0 EndY=-3.17543 EndZ=0
    g3: LineSegment StartX=0 StartY=-3.17543 StartZ=0 EndX=2.75 EndY=-1.58771 EndZ=0
    g4: LineSegment StartX=2.75 StartY=-1.58771 StartZ=0 EndX=2.75 EndY=1.58771 EndZ=0
    g5: LineSegment StartX=2.75 StartY=1.58771 StartZ=0 EndX=0 EndY=3.17543 EndZ=0
    g6: Circle [constr] CenterX=0 CenterY=0 CenterZ=0 NormalX=0 NormalY=0 NormalZ=1 AngleXU=0 Radius=3.17543
    g7: Circle CenterX=0 CenterY=0 CenterZ=0 NormalX=0 NormalY=0 NormalZ=1 AngleXU=0 Radius=1.5
  constraints (18):
    c: Coincident(g0,g1)
    c: Coincident(g1,g2)
    c: Coincident(g2,g3)
    c: Coincident(g3,g4)
    c: Coincident(g4,g5)
    c: Coincident(g5,g0)
    c: Equal(g0, g1-g5) x5
    c: PointOnObject(g0,g6)
    c: PointOnObject(g1,g6)
    c: PointOnObject(g2,g6)
    c: PointOnObject(g3,g6)
    c: PointOnObject(g4,g6)
    c: PointOnObject(g5,g6)
    c: Coincident(g6,g-1)
    c: PointOnObject(g5,g-2)
    c: DistanceX(g0,g4) = 5.5
    c: Coincident(g7,g-1)
    c: Radius(g7) = 1.5
FEATURE [Sketcher::SketchObject] Sketch1605
  MapMode = 5
  Placement = pos=(0,0,0) rot=(1,0,0;1.5708rad)
  Support = -> [XZ_Plane591]
  sketch-geometry (8):
    g0: LineSegment [constr] StartX=-4e-16 StartY=6.69726 StartZ=0 EndX=-2.9 EndY=5.02295 EndZ=0
    g1: LineSegment [constr] StartX=-2.9 StartY=5.02295 StartZ=0 EndX=-2.9 EndY=1.67432 EndZ=0
    g2: LineSegment [constr] StartX=-2.9 StartY=1.67432 StartZ=0 EndX=0 EndY=0 EndZ=0
    g3: LineSegment [constr] StartX=0 StartY=0 StartZ=0 EndX=2.9 EndY=1.67432 EndZ=0
    g4: LineSegment [constr] StartX=2.9 StartY=1.67432 StartZ=0 EndX=2.9 EndY=5.02295 EndZ=0
    g5: LineSegment [constr] StartX=2.9 StartY=5.02295 StartZ=0 EndX=-4e-16 EndY=6.69726 EndZ=0
    g6: Circle [constr] CenterX=0 CenterY=3.34863 CenterZ=0 NormalX=0 NormalY=0 NormalZ=1 AngleXU=0 Radius=3.34863
    g7: Circle CenterX=0 CenterY=3.34863 CenterZ=0 NormalX=0 NormalY=0 NormalZ=1 AngleXU=0 Radius=1.6
  constraints (18):
    c: Coincident(g0,g1)
    c: Coincident(g1,g2)
    c: Coincident(g2,g3)
    c: Coincident(g3,g4)
    c: Coincident(g4,g5)
    c: Coincident(g5,g0)
    c: Equal(g0, g1-g5) x5
    c: PointOnObject(g0,g6)
    c: PointOnObject(g1,g6)
    c: PointOnObject(g2,g6)
    c: PointOnObject(g3,g6)
    c: PointOnObject(g4,g6)
    c: PointOnObject(g5,g6)
    c: PointOnObject(g6,g-2)
    c: DistanceX(g0,g4) = 5.8
    c: Coincident(g2,g-1)
    c: Coincident(g7,g6)
    c: Radius(g7) = 1.6
FEATURE [Sketcher::SketchObject] Sketch1607
  MapMode = 5
  Support = -> [XY_Plane582]
  sketch-geometry (3):
    g0: Circle [constr] CenterX=0 CenterY=0 CenterZ=0 NormalX=0 NormalY=0 NormalZ=1 AngleXU=0 Radius=20
    g1: Circle CenterX=18.1039 CenterY=8.5 CenterZ=0 NormalX=0 NormalY=0 NormalZ=1 AngleXU=0 Radius=1.25
    g2: Circle CenterX=18.1039 CenterY=-8.5 CenterZ=0 NormalX=0 NormalY=0 NormalZ=1 AngleXU=0 Radius=1.25
  constraints (7):
    c: Coincident(g0,g-1)
    c: Radius(g0) = 20
    c: PointOnObject(g1,g0)
    c: Radius(g1) = 1.25
    c: DistanceY(g-1,g1) = 8.5
    c: Equal(g2,g1)
    c: Symmetric(g2,g1,g-1)
FEATURE [Sketcher::SketchObject] Sketch1610
  MapMode = 5
  Placement = pos=(0,0,0) rot=(1,0,0;1.5708rad)
  Support = -> [XZ_Plane591]
  sketch-geometry (2):
    g0: ArcOfCircle CenterX=0 CenterY=0 CenterZ=0 NormalX=0 NormalY=0 NormalZ=1 AngleXU=0 Radius=12.75 StartAngle=0 EndAngle=3.14159
    g1: LineSegment StartX=-12.75 StartY=0 StartZ=0 EndX=12.75 EndY=0 EndZ=0
  constraints (6):
    c: Coincident(g0,g-1)
    c: Coincident(g1,g0)
    c: Coincident(g1,g0)
    c: Horizontal(g1)
    c: PointOnObject(g0,g1)
    c: Radius(g0) = 12.75
FEATURE [Sketcher::SketchObject] Sketch1618
  MapMode = 5
  Support = -> [XY_Plane584]
  sketch-geometry (8):
    g0: LineSegment StartX=0 StartY=3.17543 StartZ=0 EndX=-2.75 EndY=1.58771 EndZ=0
    g1: LineSegment StartX=-2.75 StartY=1.58771 StartZ=0 EndX=-2.75 EndY=-1.58771 EndZ=0
    g2: LineSegment StartX=-2.75 StartY=-1.58771 StartZ=0 EndX=0 EndY=-3.17543 EndZ=0
    g3: LineSegment StartX=0 StartY=-3.17543 StartZ=0 EndX=2.75 EndY=-1.58771 EndZ=0
    g4: LineSegment StartX=2.75 StartY=-1.58771 StartZ=0 EndX=2.75 EndY=1.58771 EndZ=0
    g5: LineSegment StartX=2.75 StartY=1.58771 StartZ=0 EndX=0 EndY=3.17543 EndZ=0
    g6: Circle [constr] CenterX=0 CenterY=0 CenterZ=0 NormalX=0 NormalY=0 NormalZ=1 AngleXU=0 Radius=3.17543
    g7: Circle CenterX=0 CenterY=0 CenterZ=0 NormalX=0 NormalY=0 NormalZ=1 AngleXU=0 Radius=1.5
  constraints (18):
    c: Coincident(g0,g1)
    c: Coincident(g1,g2)
    c: Coincident(g2,g3)
    c: Coincident(g3,g4)
    c: Coincident(g4,g5)
    c: Coincident(g5,g0)
    c: Equal(g0, g1-g5) x5
    c: PointOnObject(g0,g6)
    c: PointOnObject(g1,g6)
    c: PointOnObject(g2,g6)
    c: PointOnObject(g3,g6)
    c: PointOnObject(g4,g6)
    c: PointOnObject(g5,g6)
    c: Coincident(g6,g-1)
    c: PointOnObject(g5,g-2)
    c: DistanceX(g0,g4) = 5.5
    c: Coincident(g7,g-1)
    c: Radius(g7) = 1.5
FEATURE [Sketcher::SketchObject] Sketch1624
  MapMode = 5
  Support = -> [XY_Plane587]
  sketch-geometry (1):
    g0: Circle CenterX=0 CenterY=0 CenterZ=0 NormalX=0 NormalY=0 NormalZ=1 AngleXU=0 Radius=1.9
  constraints (2):
    c: Coincident(g0,g-1)
    c: Radius(g0) = 1.9
FEATURE [Sketcher::SketchObject] Sketch1625
  MapMode = 5
  Support = -> [XY_Plane597]
  sketch-geometry (1):
    g0: Circle CenterX=0 CenterY=0 CenterZ=0 NormalX=0 NormalY=0 NormalZ=1 AngleXU=0 Radius=2.75
  constraints (2):
    c: Coincident(g0,g-1)
    c: Radius(g0) = 2.75
FEATURE [Sketcher::SketchObject] Sketch1626
  MapMode = 5
  Support = -> [XY_Plane617]
  sketch-geometry (8):
    g0: LineSegment StartX=0 StartY=3.17543 StartZ=0 EndX=-2.75 EndY=1.58771 EndZ=0
    g1: LineSegment StartX=-2.75 StartY=1.58771 StartZ=0 EndX=-2.75 EndY=-1.58771 EndZ=0
    g2: LineSegment StartX=-2.75 StartY=-1.58771 StartZ=0 EndX=0 EndY=-3.17543 EndZ=0
    g3: LineSegment StartX=0 StartY=-3.17543 StartZ=0 EndX=2.75 EndY=-1.58771 EndZ=0
    g4: LineSegment StartX=2.75 StartY=-1.58771 StartZ=0 EndX=2.75 EndY=1.58771 EndZ=0
    g5: LineSegment StartX=2.75 StartY=1.58771 StartZ=0 EndX=0 EndY=3.17543 EndZ=0
    g6: Circle [constr] CenterX=0 CenterY=0 CenterZ=0 NormalX=0 NormalY=0 NormalZ=1 AngleXU=0 Radius=3.17543
    g7: Circle CenterX=0 CenterY=0 CenterZ=0 NormalX=0 NormalY=0 NormalZ=1 AngleXU=0 Radius=1.5
  constraints (18):
    c: Coincident(g0,g1)
    c: Coincident(g1,g2)
    c: Coincident(g2,g3)
    c: Coincident(g3,g4)
    c: Coincident(g4,g5)
    c: Coincident(g5,g0)
    c: Equal(g0, g1-g5) x5
    c: PointOnObject(g0,g6)
    c: PointOnObject(g1,g6)
    c: PointOnObject(g2,g6)
    c: PointOnObject(g3,g6)
    c: PointOnObject(g4,g6)
    c: PointOnObject(g5,g6)
    c: Coincident(g6,g-1)
    c: PointOnObject(g5,g-2)
    c: DistanceX(g0,g4) = 5.5
    c: Coincident(g7,g-1)
    c: Radius(g7) = 1.5
FEATURE [Sketcher::SketchObject] Sketch1629
  MapMode = 5
  Support = -> [XY_Plane608]
  sketch-geometry (8):
    g0: LineSegment StartX=0 StartY=3.17543 StartZ=0 EndX=-2.75 EndY=1.58771 EndZ=0
    g1: LineSegment StartX=-2.75 StartY=1.58771 StartZ=0 EndX=-2.75 EndY=-1.58771 EndZ=0
    g2: LineSegment StartX=-2.75 StartY=-1.58771 StartZ=0 EndX=0 EndY=-3.17543 EndZ=0
    g3: LineSegment StartX=0 StartY=-3.17543 StartZ=0 EndX=2.75 EndY=-1.58771 EndZ=0
    g4: LineSegment StartX=2.75 StartY=-1.58771 StartZ=0 EndX=2.75 EndY=1.58771 EndZ=0
    g5: LineSegment StartX=2.75 StartY=1.58771 StartZ=0 EndX=0 EndY=3.17543 EndZ=0
    g6: Circle [constr] CenterX=0 CenterY=0 CenterZ=0 NormalX=0 NormalY=0 NormalZ=1 AngleXU=0 Radius=3.17543
    g7: Circle CenterX=0 CenterY=0 CenterZ=0 NormalX=0 NormalY=0 NormalZ=1 AngleXU=0 Radius=1.5
  constraints (18):
    c: Coincident(g0,g1)
    c: Coincident(g1,g2)
    c: Coincident(g2,g3)
    c: Coincident(g3,g4)
    c: Coincident(g4,g5)
    c: Coincident(g5,g0)
    c: Equal(g0, g1-g5) x5
    c: PointOnObject(g0,g6)
    c: PointOnObject(g1,g6)
    c: PointOnObject(g2,g6)
    c: PointOnObject(g3,g6)
    c: PointOnObject(g4,g6)
    c: PointOnObject(g5,g6)
    c: Coincident(g6,g-1)
    c: PointOnObject(g5,g-2)
    c: DistanceX(g0,g4) = 5.5
    c: Coincident(g7,g-1)
    c: Radius(g7) = 1.5
FEATURE [Sketcher::SketchObject] Sketch1636
  MapMode = 5
  Placement = pos=(0,0,0) rot=(1,0,0;1.5708rad)
  Support = -> [XZ_Plane619]
  sketch-geometry (1):
    g0: Circle CenterX=1.55 CenterY=4 CenterZ=0 NormalX=0 NormalY=0 NormalZ=1 AngleXU=0 Radius=0.75
  constraints (3):
    c: Radius(g0) = 0.75
    c: DistanceY(g-1,g0) = 4
    c: DistanceX(g-1,g0) = 1.55
FEATURE [Sketcher::SketchObject] Sketch1637
  MapMode = 5
  Support = -> [XY_Plane616]
  sketch-geometry (8):
    g0: LineSegment StartX=0 StartY=3.17543 StartZ=0 EndX=-2.75 EndY=1.58771 EndZ=0
    g1: LineSegment StartX=-2.75 StartY=1.58771 StartZ=0 EndX=-2.75 EndY=-1.58771 EndZ=0
    g2: LineSegment StartX=-2.75 StartY=-1.58771 StartZ=0 EndX=0 EndY=-3.17543 EndZ=0
    g3: LineSegment StartX=0 StartY=-3.17543 StartZ=0 EndX=2.75 EndY=-1.58771 EndZ=0
    g4: LineSegment StartX=2.75 StartY=-1.58771 StartZ=0 EndX=2.75 EndY=1.58771 EndZ=0
    g5: LineSegment StartX=2.75 StartY=1.58771 StartZ=0 EndX=0 EndY=3.17543 EndZ=0
    g6: Circle [constr] CenterX=0 CenterY=0 CenterZ=0 NormalX=0 NormalY=0 NormalZ=1 AngleXU=0 Radius=3.17543
    g7: Circle CenterX=0 CenterY=0 CenterZ=0 NormalX=0 NormalY=0 NormalZ=1 AngleXU=0 Radius=1.5
  constraints (18):
    c: Coincident(g0,g1)
    c: Coincident(g1,g2)
    c: Coincident(g2,g3)
    c: Coincident(g3,g4)
    c: Coincident(g4,g5)
    c: Coincident(g5,g0)
    c: Equal(g0, g1-g5) x5
    c: PointOnObject(g0,g6)
    c: PointOnObject(g1,g6)
    c: PointOnObject(g2,g6)
    c: PointOnObject(g3,g6)
    c: PointOnObject(g4,g6)
    c: PointOnObject(g5,g6)
    c: Coincident(g6,g-1)
    c: PointOnObject(g5,g-2)
    c: DistanceX(g0,g4) = 5.5
    c: Coincident(g7,g-1)
    c: Radius(g7) = 1.5
FEATURE [Sketcher::SketchObject] Sketch1638
  MapMode = 5
  Support = -> [XY_Plane676]
  sketch-geometry (1):
    g0: Circle CenterX=0 CenterY=0 CenterZ=0 NormalX=0 NormalY=0 NormalZ=1 AngleXU=0 Radius=2.75
  constraints (2):
    c: Coincident(g0,g-1)
    c: Radius(g0) = 2.75
FEATURE [Sketcher::SketchObject] Sketch1640
  MapMode = 5
  Support = -> [XY_Plane614]
  sketch-geometry (8):
    g0: LineSegment StartX=0 StartY=3.17543 StartZ=0 EndX=-2.75 EndY=1.58771 EndZ=0
    g1: LineSegment StartX=-2.75 StartY=1.58771 StartZ=0 EndX=-2.75 EndY=-1.58771 EndZ=0
    g2: LineSegment StartX=-2.75 StartY=-1.58771 StartZ=0 EndX=0 EndY=-3.17543 EndZ=0
    g3: LineSegment StartX=0 StartY=-3.17543 StartZ=0 EndX=2.75 EndY=-1.58771 EndZ=0
    g4: LineSegment StartX=2.75 StartY=-1.58771 StartZ=0 EndX=2.75 EndY=1.58771 EndZ=0
    g5: LineSegment StartX=2.75 StartY=1.58771 StartZ=0 EndX=0 EndY=3.17543 EndZ=0
    g6: Circle [constr] CenterX=0 CenterY=0 CenterZ=0 NormalX=0 NormalY=0 NormalZ=1 AngleXU=0 Radius=3.17543
    g7: Circle CenterX=0 CenterY=0 CenterZ=0 NormalX=0 NormalY=0 NormalZ=1 AngleXU=0 Radius=1.5
  constraints (18):
    c: Coincident(g0,g1)
    c: Coincident(g1,g2)
    c: Coincident(g2,g3)
    c: Coincident(g3,g4)
    c: Coincident(g4,g5)
    c: Coincident(g5,g0)
    c: Equal(g0, g1-g5) x5
    c: PointOnObject(g0,g6)
    c: PointOnObject(g1,g6)
    c: PointOnObject(g2,g6)
    c: PointOnObject(g3,g6)
    c: PointOnObject(g4,g6)
    c: PointOnObject(g5,g6)
    c: Coincident(g6,g-1)
    c: PointOnObject(g5,g-2)
    c: DistanceX(g0,g4) = 5.5
    c: Coincident(g7,g-1)
    c: Radius(g7) = 1.5
FEATURE [Sketcher::SketchObject] Sketch1642
  MapMode = 5
  Support = -> [XY_Plane623]
  sketch-geometry (4):
    g0: LineSegment StartX=-10 StartY=20.15 StartZ=0 EndX=10 EndY=20.15 EndZ=0
    g1: LineSegment StartX=10 StartY=20.15 StartZ=0 EndX=10 EndY=-20.15 EndZ=0
    g2: LineSegment StartX=10 StartY=-20.15 StartZ=0 EndX=-10 EndY=-20.15 EndZ=0
    g3: LineSegment StartX=-10 StartY=-20.15 StartZ=0 EndX=-10 EndY=20.15 EndZ=0
  constraints (10):
    c: Coincident(g0,g1)
    c: Coincident(g1,g2)
    c: Coincident(g2,g3)
    c: Coincident(g3,g0)
    c: Horizontal(g2)
    c: Vertical(g3)
    c: DistanceX(g0,g0) = 20
    c: DistanceY(g1,g1) = 40.3
    c: Symmetric(g0,g1,g-1)
    c: Symmetric(g0,g0,g-2)
FEATURE [Sketcher::SketchObject] Sketch1644
  MapMode = 5
  Support = -> [XY_Plane633]
  sketch-geometry (1):
    g0: Circle CenterX=0 CenterY=10.15 CenterZ=0 NormalX=0 NormalY=0 NormalZ=1 AngleXU=0 Radius=3
  constraints (3):
    c: PointOnObject(g0,g-2)
    c: DistanceY(g-1,g0) = 10.15
    c: Radius(g0) = 3
FEATURE [Sketcher::SketchObject] Sketch1646
  MapMode = 5
  Placement = pos=(0,0,0) rot=(1,0,0;1.5708rad)
  Support = -> [XZ_Plane632]
  sketch-geometry (1):
    g0: Circle CenterX=-1.55 CenterY=4 CenterZ=0 NormalX=0 NormalY=0 NormalZ=1 AngleXU=0 Radius=0.75
  constraints (3):
    c: Radius(g0) = 0.75
    c: DistanceY(g-1,g0) = 4
    c: DistanceX(g0,g-1) = 1.55
FEATURE [Sketcher::SketchObject] Sketch1650
  MapMode = 5
  Support = -> [XY_Plane635]
  sketch-geometry (1):
    g0: Circle CenterX=0 CenterY=0 CenterZ=0 NormalX=0 NormalY=0 NormalZ=1 AngleXU=0 Radius=2.75
  constraints (2):
    c: Coincident(g0,g-1)
    c: Radius(g0) = 2.75
FEATURE [Sketcher::SketchObject] Sketch1651
  MapMode = 5
  Placement = pos=(0,0,0) rot=(1,0,0;1.5708rad)
  Support = -> [XZ_Plane630]
  sketch-geometry (1):
    g0: Circle CenterX=0 CenterY=4 CenterZ=0 NormalX=0 NormalY=0 NormalZ=1 AngleXU=0 Radius=0.75
  constraints (3):
    c: PointOnObject(g0,g-2)
    c: Radius(g0) = 0.75
    c: DistanceY(g-1,g0) = 4
FEATURE [Sketcher::SketchObject] Sketch1652
  MapMode = 5
  Support = -> [XY_Plane620]
  sketch-geometry (1):
    g0: Circle CenterX=0 CenterY=0 CenterZ=0 NormalX=0 NormalY=0 NormalZ=1 AngleXU=0 Radius=2.75
  constraints (2):
    c: Coincident(g0,g-1)
    c: Radius(g0) = 2.75
FEATURE [Sketcher::SketchObject] Sketch1653
  MapMode = 5
  Support = -> [XY_Plane669]
  sketch-geometry (1):
    g0: Circle CenterX=0 CenterY=0 CenterZ=0 NormalX=0 NormalY=0 NormalZ=1 AngleXU=0 Radius=2.75
  constraints (2):
    c: Coincident(g0,g-1)
    c: Radius(g0) = 2.75
FEATURE [Sketcher::SketchObject] Sketch1660
  MapMode = 5
  Support = -> [XY_Plane679]
  sketch-geometry (8):
    g0: LineSegment StartX=0 StartY=2.3094 StartZ=0 EndX=-2 EndY=1.1547 EndZ=0
    g1: LineSegment StartX=-2 StartY=1.1547 StartZ=0 EndX=-2 EndY=-1.1547 EndZ=0
    g2: LineSegment StartX=-2 StartY=-1.1547 StartZ=0 EndX=-2e-16 EndY=-2.3094 EndZ=0
    g3: LineSegment StartX=-2e-16 StartY=-2.3094 StartZ=0 EndX=2 EndY=-1.1547 EndZ=0
    g4: LineSegment StartX=2 StartY=-1.1547 StartZ=0 EndX=2 EndY=1.1547 EndZ=0
    g5: LineSegment StartX=2 StartY=1.1547 StartZ=0 EndX=0 EndY=2.3094 EndZ=0
    g6: Circle [constr] CenterX=0 CenterY=0 CenterZ=0 NormalX=0 NormalY=0 NormalZ=1 AngleXU=0 Radius=2.3094
    g7: Circle CenterX=0 CenterY=0 CenterZ=0 NormalX=0 NormalY=0 NormalZ=1 AngleXU=0 Radius=1
  constraints (18):
    c: Coincident(g0,g1)
    c: Coincident(g1,g2)
    c: Coincident(g2,g3)
    c: Coincident(g3,g4)
    c: Coincident(g4,g5)
    c: Coincident(g5,g0)
    c: Equal(g0, g1-g5) x5
    c: PointOnObject(g0,g6)
    c: PointOnObject(g1,g6)
    c: PointOnObject(g2,g6)
    c: PointOnObject(g3,g6)
    c: PointOnObject(g4,g6)
    c: PointOnObject(g5,g6)
    c: Coincident(g6,g-1)
    c: PointOnObject(g5,g-2)
    c: DistanceX(g0,g4) = 4
    c: Coincident(g7,g-1)
    c: Radius(g7) = 1
FEATURE [Sketcher::SketchObject] Sketch1662
  MapMode = 5
  Support = -> [XY_Plane654]
  sketch-geometry (8):
    g0: LineSegment StartX=0 StartY=2.3094 StartZ=0 EndX=-2 EndY=1.1547 EndZ=0
    g1: LineSegment StartX=-2 StartY=1.1547 StartZ=0 EndX=-2 EndY=-1.1547 EndZ=0
    g2: LineSegment StartX=-2 StartY=-1.1547 StartZ=0 EndX=-2e-16 EndY=-2.3094 EndZ=0
    g3: LineSegment StartX=-2e-16 StartY=-2.3094 StartZ=0 EndX=2 EndY=-1.1547 EndZ=0
    g4: LineSegment StartX=2 StartY=-1.1547 StartZ=0 EndX=2 EndY=1.1547 EndZ=0
    g5: LineSegment StartX=2 StartY=1.1547 StartZ=0 EndX=0 EndY=2.3094 EndZ=0
    g6: Circle [constr] CenterX=0 CenterY=0 CenterZ=0 NormalX=0 NormalY=0 NormalZ=1 AngleXU=0 Radius=2.3094
    g7: Circle CenterX=0 CenterY=0 CenterZ=0 NormalX=0 NormalY=0 NormalZ=1 AngleXU=0 Radius=1
  constraints (18):
    c: Coincident(g0,g1)
    c: Coincident(g1,g2)
    c: Coincident(g2,g3)
    c: Coincident(g3,g4)
    c: Coincident(g4,g5)
    c: Coincident(g5,g0)
    c: Equal(g0, g1-g5) x5
    c: PointOnObject(g0,g6)
    c: PointOnObject(g1,g6)
    c: PointOnObject(g2,g6)
    c: PointOnObject(g3,g6)
    c: PointOnObject(g4,g6)
    c: PointOnObject(g5,g6)
    c: Coincident(g6,g-1)
    c: PointOnObject(g5,g-2)
    c: DistanceX(g0,g4) = 4
    c: Coincident(g7,g-1)
    c: Radius(g7) = 1
FEATURE [Sketcher::SketchObject] Sketch1663
  MapMode = 5
  Support = -> [XY_Plane646]
  sketch-geometry (1):
    g0: Circle CenterX=0 CenterY=0 CenterZ=0 NormalX=0 NormalY=0 NormalZ=1 AngleXU=0 Radius=1.9
  constraints (2):
    c: Coincident(g0,g-1)
    c: Radius(g0) = 1.9
FEATURE [Sketcher::SketchObject] Sketch1667
  MapMode = 5
  Support = -> [XY_Plane660]
  sketch-geometry (8):
    g0: LineSegment StartX=0 StartY=2.3094 StartZ=0 EndX=-2 EndY=1.1547 EndZ=0
    g1: LineSegment StartX=-2 StartY=1.1547 StartZ=0 EndX=-2 EndY=-1.1547 EndZ=0
    g2: LineSegment StartX=-2 StartY=-1.1547 StartZ=0 EndX=-2e-16 EndY=-2.3094 EndZ=0
    g3: LineSegment StartX=-2e-16 StartY=-2.3094 StartZ=0 EndX=2 EndY=-1.1547 EndZ=0
    g4: LineSegment StartX=2 StartY=-1.1547 StartZ=0 EndX=2 EndY=1.1547 EndZ=0
    g5: LineSegment StartX=2 StartY=1.1547 StartZ=0 EndX=0 EndY=2.3094 EndZ=0
    g6: Circle [constr] CenterX=0 CenterY=0 CenterZ=0 NormalX=0 NormalY=0 NormalZ=1 AngleXU=0 Radius=2.3094
    g7: Circle CenterX=0 CenterY=0 CenterZ=0 NormalX=0 NormalY=0 NormalZ=1 AngleXU=0 Radius=1
  constraints (18):
    c: Coincident(g0,g1)
    c: Coincident(g1,g2)
    c: Coincident(g2,g3)
    c: Coincident(g3,g4)
    c: Coincident(g4,g5)
    c: Coincident(g5,g0)
    c: Equal(g0, g1-g5) x5
    c: PointOnObject(g0,g6)
    c: PointOnObject(g1,g6)
    c: PointOnObject(g2,g6)
    c: PointOnObject(g3,g6)
    c: PointOnObject(g4,g6)
    c: PointOnObject(g5,g6)
    c: Coincident(g6,g-1)
    c: PointOnObject(g5,g-2)
    c: DistanceX(g0,g4) = 4
    c: Coincident(g7,g-1)
    c: Radius(g7) = 1
FEATURE [Sketcher::SketchObject] Sketch1668
  MapMode = 5
  Support = -> [XY_Plane682]
  sketch-geometry (1):
    g0: Circle CenterX=0 CenterY=0 CenterZ=0 NormalX=0 NormalY=0 NormalZ=1 AngleXU=0 Radius=1.9
  constraints (2):
    c: Coincident(g0,g-1)
    c: Radius(g0) = 1.9
FEATURE [Sketcher::SketchObject] Sketch1671
  MapMode = 5
  Support = -> [XY_Plane645]
  sketch-geometry (1):
    g0: Circle CenterX=0 CenterY=0 CenterZ=0 NormalX=0 NormalY=0 NormalZ=1 AngleXU=0 Radius=1.9
  constraints (2):
    c: Coincident(g0,g-1)
    c: Radius(g0) = 1.9
FEATURE [Sketcher::SketchObject] Sketch1672
  MapMode = 5
  Support = -> [XY_Plane648]
  sketch-geometry (8):
    g0: LineSegment StartX=0 StartY=2.3094 StartZ=0 EndX=-2 EndY=1.1547 EndZ=0
    g1: LineSegment StartX=-2 StartY=1.1547 StartZ=0 EndX=-2 EndY=-1.1547 EndZ=0
    g2: LineSegment StartX=-2 StartY=-1.1547 StartZ=0 EndX=-2e-16 EndY=-2.3094 EndZ=0
    g3: LineSegment StartX=-2e-16 StartY=-2.3094 StartZ=0 EndX=2 EndY=-1.1547 EndZ=0
    g4: LineSegment StartX=2 StartY=-1.1547 StartZ=0 EndX=2 EndY=1.1547 EndZ=0
    g5: LineSegment StartX=2 StartY=1.1547 StartZ=0 EndX=0 EndY=2.3094 EndZ=0
    g6: Circle [constr] CenterX=0 CenterY=0 CenterZ=0 NormalX=0 NormalY=0 NormalZ=1 AngleXU=0 Radius=2.3094
    g7: Circle CenterX=0 CenterY=0 CenterZ=0 NormalX=0 NormalY=0 NormalZ=1 AngleXU=0 Radius=1
  constraints (18):
    c: Coincident(g0,g1)
    c: Coincident(g1,g2)
    c: Coincident(g2,g3)
    c: Coincident(g3,g4)
    c: Coincident(g4,g5)
    c: Coincident(g5,g0)
    c: Equal(g0, g1-g5) x5
    c: PointOnObject(g0,g6)
    c: PointOnObject(g1,g6)
    c: PointOnObject(g2,g6)
    c: PointOnObject(g3,g6)
    c: PointOnObject(g4,g6)
    c: PointOnObject(g5,g6)
    c: Coincident(g6,g-1)
    c: PointOnObject(g5,g-2)
    c: DistanceX(g0,g4) = 4
    c: Coincident(g7,g-1)
    c: Radius(g7) = 1
FEATURE [Sketcher::SketchObject] Sketch1676
  MapMode = 5
  Support = -> [XY_Plane679]
FEATURE [Sketcher::SketchObject] Sketch1677
  MapMode = 5
  Support = -> [XY_Plane648]
FEATURE [Sketcher::SketchObject] Sketch1680
  MapMode = 5
  Support = -> [XY_Plane644]
  sketch-geometry (1):
    g0: Circle CenterX=0 CenterY=0 CenterZ=0 NormalX=0 NormalY=0 NormalZ=1 AngleXU=0 Radius=2.75
  constraints (2):
    c: Coincident(g0,g-1)
    c: Radius(g0) = 2.75
FEATURE [Sketcher::SketchObject] Sketch1682
  MapMode = 5
  Placement = pos=(0,0,0) rot=(1,0,0;1.5708rad)
  Support = -> [XZ_Plane591]
  sketch-geometry (2):
    g0: Circle [constr] CenterX=0 CenterY=0 CenterZ=0 NormalX=0 NormalY=0 NormalZ=1 AngleXU=0 Radius=20
    g1: Circle CenterX=-20 CenterY=0 CenterZ=0 NormalX=0 NormalY=0 NormalZ=1 AngleXU=0 Radius=1.25
  constraints (5):
    c: Coincident(g0,g-1)
    c: Radius(g0) = 20
    c: PointOnObject(g1,g0)
    c: Radius(g1) = 1.25
    c: PointOnObject(g1,g-1)
FEATURE [Sketcher::SketchObject] Sketch1713
  MapMode = 5
  Support = -> [XY_Plane649]
FEATURE [Sketcher::SketchObject] Sketch1715
  MapMode = 5
  Support = -> [XY_Plane657]
  sketch-geometry (64):
    g0: LineSegment [constr] StartX=-3.75 StartY=6.49519 StartZ=0 EndX=-7.5 EndY=0 EndZ=0
    g1: LineSegment [constr] StartX=-7.5 StartY=0 StartZ=0 EndX=-3.75 EndY=-6.49519 EndZ=0
    g2: LineSegment [constr] StartX=-3.75 StartY=-6.49519 StartZ=0 EndX=3.75 EndY=-6.49519 EndZ=0
    g3: LineSegment [constr] StartX=3.75 StartY=-6.49519 StartZ=0 EndX=7.5 EndY=0 EndZ=0
    g4: LineSegment [constr] StartX=7.5 StartY=0 StartZ=0 EndX=3.75 EndY=6.49519 EndZ=0
    g5: LineSegment [constr] StartX=3.75 StartY=6.49519 StartZ=0 EndX=-3.75 EndY=6.49519 EndZ=0
    g6: Circle [constr] CenterX=0 CenterY=0 CenterZ=0 NormalX=0 NormalY=0 NormalZ=1 AngleXU=0 Radius=7.5
    g7: LineSegment [constr] StartX=0 StartY=7.5 StartZ=0 EndX=-6.49519 EndY=3.75 EndZ=0
    g8: LineSegment [constr] StartX=-6.49519 StartY=3.75 StartZ=0 EndX=-6.49519 EndY=-3.75 EndZ=0
    g9: LineSegment [constr] StartX=-6.49519 StartY=-3.75 StartZ=0 EndX=9.8e-15 EndY=-7.5 EndZ=0
    g10: LineSegment [constr] StartX=9.8e-15 StartY=-7.5 StartZ=0 EndX=6.49519 EndY=-3.75 EndZ=0
    g11: LineSegment [constr] StartX=6.49519 StartY=-3.75 StartZ=0 EndX=6.49519 EndY=3.75 EndZ=0
    g12: LineSegment [constr] StartX=6.49519 StartY=3.75 StartZ=0 EndX=0 EndY=7.5 EndZ=0
    g13: Circle [constr] CenterX=0 CenterY=0 CenterZ=0 NormalX=0 NormalY=0 NormalZ=1 AngleXU=0 Radius=7.5
    g14: LineSegment [constr] StartX=0 StartY=10.5 StartZ=0 EndX=-9.09327 EndY=5.25 EndZ=0
    g15: LineSegment [constr] StartX=-9.09327 StartY=5.25 StartZ=0 EndX=-9.09327 EndY=-5.25 EndZ=0
    g16: LineSegment [constr] StartX=-9.09327 StartY=-5.25 StartZ=0 EndX=-1.42e-14 EndY=-10.5 EndZ=0
    g17: LineSegment [constr] StartX=-1.42e-14 StartY=-10.5 StartZ=0 EndX=9.09327 EndY=-5.25 EndZ=0
    g18: LineSegment [constr] StartX=9.09327 StartY=-5.25 StartZ=0 EndX=9.09327 EndY=5.25 EndZ=0
    g19: LineSegment [constr] StartX=9.09327 StartY=5.25 StartZ=0 EndX=0 EndY=10.5 EndZ=0
    g20: Circle [constr] CenterX=0 CenterY=0 CenterZ=0 NormalX=0 NormalY=0 NormalZ=1 AngleXU=0 Radius=10.5
    g21: LineSegment [constr] StartX=0 StartY=13.5 StartZ=0 EndX=-11.6913 EndY=6.75 EndZ=0
    g22: LineSegment [constr] StartX=-11.6913 StartY=6.75 StartZ=0 EndX=-11.6913 EndY=-6.75 EndZ=0
    g23: LineSegment [constr] StartX=-11.6913 StartY=-6.75 StartZ=0 EndX=0 EndY=-13.5 EndZ=0
    g24: LineSegment [constr] StartX=0 StartY=-13.5 StartZ=0 EndX=11.6913 EndY=-6.75 EndZ=0
    g25: LineSegment [constr] StartX=11.6913 StartY=-6.75 StartZ=0 EndX=11.6913 EndY=6.75 EndZ=0
    g26: LineSegment [constr] StartX=11.6913 StartY=6.75 StartZ=0 EndX=0 EndY=13.5 EndZ=0
    g27: Circle [constr] CenterX=0 CenterY=0 CenterZ=0 NormalX=0 NormalY=0 NormalZ=1 AngleXU=0 Radius=13.5
    g28: ArcOfCircle CenterX=0 CenterY=13.5 CenterZ=0 NormalX=0 NormalY=0 NormalZ=1 AngleXU=0 Radius=2.5 StartAngle=0.171439 EndAngle=2.97015
    g29: ArcOfCircle CenterX=11.6913 CenterY=6.75 CenterZ=0 NormalX=0 NormalY=0 NormalZ=1 AngleXU=0 Radius=2.5 StartAngle=5.40743 EndAngle=8.20614
    g30: ArcOfCircle CenterX=11.6913 CenterY=-6.75 CenterZ=0 NormalX=0 NormalY=0 NormalZ=1 AngleXU=0 Radius=2.5 StartAngle=4.36023 EndAngle=7.15894
    g31: ArcOfCircle CenterX=0 CenterY=-13.5 CenterZ=0 NormalX=0 NormalY=0 NormalZ=1 AngleXU=0 Radius=2.5 StartAngle=3.31303 EndAngle=6.11175
    g32: ArcOfCircle CenterX=-11.6913 CenterY=-6.75 CenterZ=0 NormalX=0 NormalY=0 NormalZ=1 AngleXU=0 Radius=2.5 StartAngle=2.26583 EndAngle=5.06455
    g33: ArcOfCircle CenterX=-11.6913 CenterY=6.75 CenterZ=0 NormalX=0 NormalY=0 NormalZ=1 AngleXU=0 Radius=2.5 StartAngle=1.21864 EndAngle=4.01735
    g34: LineSegment StartX=-10.829 StartY=9.09658 StartZ=0 EndX=-3.75 EndY=6.49519 EndZ=0
    g35: LineSegment StartX=-3.75 StartY=6.49519 StartZ=0 EndX=-2.46335 EndY=13.9265 EndZ=0
    g36: LineSegment StartX=2.46335 StartY=13.9265 StartZ=0 EndX=3.75 EndY=6.49519 EndZ=0
    g37: LineSegment StartX=3.75 StartY=6.49519 StartZ=0 EndX=10.829 EndY=9.09658 EndZ=0
    g38: LineSegment StartX=13.2924 StartY=4.82993 StartZ=0 EndX=7.5 EndY=0 EndZ=0
    g39: LineSegment StartX=7.5 StartY=0 StartZ=0 EndX=13.2924 EndY=-4.82993 EndZ=0
    g40: LineSegment StartX=10.829 StartY=-9.09658 StartZ=0 EndX=3.75 EndY=-6.49519 EndZ=0
    g41: LineSegment StartX=3.75 StartY=-6.49519 StartZ=0 EndX=2.46335 EndY=-13.9265 EndZ=0
    g42: LineSegment StartX=-2.46335 StartY=-13.9265 StartZ=0 EndX=-3.75 EndY=-6.49519 EndZ=0
    g43: LineSegment StartX=-3.75 StartY=-6.49519 StartZ=0 EndX=-10.829 EndY=-9.09658 EndZ=0
    g44: LineSegment StartX=-13.2924 StartY=-4.82993 StartZ=0 EndX=-7.5 EndY=0 EndZ=0
    g45: LineSegment StartX=-7.5 StartY=0 StartZ=0 EndX=-13.2924 EndY=4.82993 EndZ=0
    g46: Circle CenterX=-11.6913 CenterY=6.75 CenterZ=0 NormalX=0 NormalY=0 NormalZ=1 AngleXU=0 Radius=0.75
    g47: Circle CenterX=-9.09327 CenterY=5.25 CenterZ=0 NormalX=0 NormalY=0 NormalZ=1 AngleXU=0 Radius=0.75
    g48: Circle CenterX=-6.49519 CenterY=3.75 CenterZ=0 NormalX=0 NormalY=0 NormalZ=1 AngleXU=0 Radius=0.75
    g49: Circle CenterX=0 CenterY=13.5 CenterZ=0 NormalX=0 NormalY=0 NormalZ=1 AngleXU=0 Radius=0.75
    g50: Circle CenterX=0 CenterY=10.5 CenterZ=0 NormalX=0 NormalY=0 NormalZ=1 AngleXU=0 Radius=0.75
    g51: Circle CenterX=0 CenterY=7.5 CenterZ=0 NormalX=0 NormalY=0 NormalZ=1 AngleXU=0 Radius=0.75
    g52: Circle CenterX=11.6913 CenterY=6.75 CenterZ=0 NormalX=0 NormalY=0 NormalZ=1 AngleXU=0 Radius=0.75
    g53: Circle CenterX=9.09327 CenterY=5.25 CenterZ=0 NormalX=0 NormalY=0 NormalZ=1 AngleXU=0 Radius=0.75
    g54: Circle CenterX=6.49519 CenterY=3.75 CenterZ=0 NormalX=0 NormalY=0 NormalZ=1 AngleXU=0 Radius=0.75
    g55: Circle CenterX=11.6913 CenterY=-6.75 CenterZ=0 NormalX=0 NormalY=0 NormalZ=1 AngleXU=0 Radius=0.75
    g56: Circle CenterX=9.09327 CenterY=-5.25 CenterZ=0 NormalX=0 NormalY=0 NormalZ=1 AngleXU=0 Radius=0.75
    g57: Circle CenterX=6.49519 CenterY=-3.75 CenterZ=0 NormalX=0 NormalY=0 NormalZ=1 AngleXU=0 Radius=0.75
    g58: Circle CenterX=9.8e-15 CenterY=-7.5 CenterZ=0 NormalX=0 NormalY=0 NormalZ=1 AngleXU=0 Radius=0.75
    g59: Circle CenterX=-1.42e-14 CenterY=-10.5 CenterZ=0 NormalX=0 NormalY=0 NormalZ=1 AngleXU=0 Radius=0.75
    g60: Circle CenterX=0 CenterY=-13.5 CenterZ=0 NormalX=0 NormalY=0 NormalZ=1 AngleXU=0 Radius=0.75
    g61: Circle CenterX=-11.6913 CenterY=-6.75 CenterZ=0 NormalX=0 NormalY=0 NormalZ=1 AngleXU=0 Radius=0.75
    g62: Circle CenterX=-9.09327 CenterY=-5.25 CenterZ=0 NormalX=0 NormalY=0 NormalZ=1 AngleXU=0 Radius=0.75
    g63: Circle CenterX=-6.49519 CenterY=-3.75 CenterZ=0 NormalX=0 NormalY=0 NormalZ=1 AngleXU=0 Radius=0.75
  constraints (136):
    c: Coincident(g0,g1)
    c: Coincident(g1,g2)
    c: Coincident(g2,g3)
    c: Coincident(g3,g4)
    c: Coincident(g4,g5)
    c: Coincident(g5,g0)
    c: Equal(g0, g1-g5) x5
    c: PointOnObject(g0,g6)
    c: PointOnObject(g1,g6)
    c: PointOnObject(g2,g6)
    c: PointOnObject(g3,g6)
    c: PointOnObject(g4,g6)
    c: PointOnObject(g5,g6)
    c: Coincident(g6,g-1)
    c: Coincident(g7,g8)
    c: Coincident(g8,g9)
    c: Coincident(g9,g10)
    c: Coincident(g10,g11)
    c: Coincident(g11,g12)
    c: Coincident(g12,g7)
    c: Equal(g7, g8-g12) x5
    c: PointOnObject(g7,g13)
    c: PointOnObject(g8,g13)
    c: PointOnObject(g9,g13)
    c: PointOnObject(g10,g13)
    c: PointOnObject(g11,g13)
    c: PointOnObject(g12,g13)
    c: Coincident(g13,g-1)
    c: PointOnObject(g12,g6)
    c: PointOnObject(g7,g-2)
    c: Horizontal(g5)
    c: Radius(g6) = 7.5
    c: Coincident(g14,g15)
    c: Coincident(g15,g16)
    c: Coincident(g16,g17)
    c: Coincident(g17,g18)
    c: Coincident(g18,g19)
    c: Coincident(g19,g14)
    c: Equal(g14, g15-g19) x5
    c: PointOnObject(g14,g20)
    c: PointOnObject(g15,g20)
    c: PointOnObject(g16,g20)
    c: PointOnObject(g17,g20)
    c: PointOnObject(g18,g20)
    c: PointOnObject(g19,g20)
    c: Coincident(g20,g-1)
    c: PointOnObject(g19,g-2)
    c: Radius(g20) = 10.5
    c: Coincident(g21,g22)
    c: Coincident(g22,g23)
    c: Coincident(g23,g24)
    c: Coincident(g24,g25)
    c: Coincident(g25,g26)
    c: Coincident(g26,g21)
    c: Equal(g21, g22-g26) x5
    c: PointOnObject(g21,g27)
    c: PointOnObject(g22,g27)
    c: PointOnObject(g23,g27)
    c: PointOnObject(g24,g27)
    c: PointOnObject(g25,g27)
    c: PointOnObject(g26,g27)
    c: Coincident(g27,g-1)
    c: PointOnObject(g26,g-2)
    c: Radius(g27) = 13.5
    c: Coincident(g28,g21)
    c: Coincident(g29,g25)
    c: Coincident(g30,g24)
    c: Coincident(g31,g23)
    c: Coincident(g32,g22)
    c: Coincident(g33,g21)
    c: Coincident(g34,g0)
    c: Coincident(g35,g34)
    c: Coincident(g36,g4)
    c: Coincident(g37,g36)
    c: Coincident(g38,g3)
    c: Coincident(g39,g38)
    c: Coincident(g40,g2)
    c: Coincident(g41,g40)
    c: Coincident(g42,g1)
    c: Coincident(g43,g42)
    c: Coincident(g44,g0)
    c: Coincident(g45,g44)
    c: Tangent(g35,g28) = 1.5708
    c: Tangent(g36,g28) = 1.5708
    c: Tangent(g37,g29) = 1.5708
    c: Tangent(g38,g29) = 1.5708
    c: Tangent(g39,g30) = 1.5708
    c: Tangent(g40,g30) = 1.5708
    c: Tangent(g41,g31) = 1.5708
    c: Tangent(g42,g31) = 1.5708
    c: Tangent(g43,g32) = 1.5708
    c: Tangent(g44,g32) = 1.5708
    c: Tangent(g45,g33) = 1.5708
    c: Tangent(g34,g33) = 1.5708
    c: Radius(g29) = 2.5
    c: Equal(g29,g28)
    c: Equal(g28,g33)
    c: Equal(g33,g32)
    c: Equal(g32,g31)
    c: Equal(g31,g30)
    c: Coincident(g46,g33)
    c: Coincident(g47,g14)
    c: Coincident(g48,g7)
    c: Coincident(g49,g28)
    c: Coincident(g50,g14)
    c: Coincident(g51,g7)
    c: Coincident(g52,g29)
    c: Coincident(g53,g18)
    c: Coincident(g54,g11)
    c: Coincident(g55,g30)
    c: Coincident(g56,g17)
    c: Coincident(g57,g10)
    c: Coincident(g58,g9)
    c: Coincident(g59,g16)
    c: Coincident(g60,g31)
    c: Coincident(g61,g32)
    c: Coincident(g62,g15)
    c: Coincident(g63,g8)
    c: Equal(g61,g62)
    c: Equal(g62,g63)
    c: Equal(g63,g58)
    c: Equal(g58,g59)
    c: Equal(g59,g60)
    c: Equal(g60,g55)
    c: Equal(g55,g56)
    c: Equal(g56,g57)
    c: Equal(g57,g54)
    c: Equal(g54,g53)
    c: Equal(g53,g52)
    c: Equal(g52,g51)
    c: Equal(g51,g50)
    c: Equal(g50,g49)
    c: Equal(g49,g46)
    c: Equal(g46,g47)
    c: Equal(g47,g48)
    c: Radius(g55) = 0.75
FEATURE [Sketcher::SketchObject] Sketch1716
  MapMode = 5
  Support = -> [XY_Plane649]
FEATURE [Sketcher::SketchObject] Sketch1718
  MapMode = 5
  Placement = pos=(0,0,0) rot=(1,0,0;1.5708rad)
  Support = -> [XZ_Plane687]
  sketch-geometry (8):
    g0: LineSegment StartX=-1.5 StartY=2.25 StartZ=0 EndX=-3.25 EndY=2.25 EndZ=0
    g1: LineSegment StartX=-3.25 StartY=2.25 StartZ=0 EndX=-3.25 EndY=1.25 EndZ=0
    g2: LineSegment StartX=-3.25 StartY=1.25 StartZ=0 EndX=-2 EndY=1.25 EndZ=0
    g3: LineSegment StartX=-2 StartY=1.25 StartZ=0 EndX=-2 EndY=-1.25 EndZ=0
    g4: LineSegment StartX=-2 StartY=-1.25 StartZ=0 EndX=-3.25 EndY=-1.25 EndZ=0
    g5: LineSegment StartX=-3.25 StartY=-1.25 StartZ=0 EndX=-3.25 EndY=-2.25 EndZ=0
    g6: LineSegment StartX=-3.25 StartY=-2.25 StartZ=0 EndX=-1.5 EndY=-2.25 EndZ=0
    g7: LineSegment StartX=-1.5 StartY=-2.25 StartZ=0 EndX=-1.5 EndY=2.25 EndZ=0
  constraints (23):
    c: Horizontal(g0)
    c: Coincident(g0,g1)
    c: Vertical(g1)
    c: Coincident(g1,g2)
    c: Horizontal(g2)
    c: Coincident(g2,g3)
    c: Vertical(g3)
    c: Coincident(g3,g4)
    c: Horizontal(g4)
    c: Coincident(g4,g5)
    c: Vertical(g5)
    c: Coincident(g5,g6)
    c: Horizontal(g6)
    c: Coincident(g6,g7)
    c: Vertical(g7)
    c: Coincident(g0,g7)
    c: Equal(g1,g5)
    c: Symmetric(g4,g1,g-1)
    c: DistanceX(g0,g-1) = 1.5
    c: DistanceY(g3,g3) = 2.5
    c: DistanceY(g7,g7) = 4.5
    c: DistanceX(g0,g-1) = 3.25
    c: DistanceX(g2,g-1) = 2
FEATURE [Sketcher::SketchObject] Sketch1722
  MapMode = 5
  Support = -> [XY_Plane660]
FEATURE [Sketcher::SketchObject] Sketch1730
  MapMode = 5
  Support = -> [XY_Plane654]
FEATURE [Sketcher::SketchObject] Sketch1731
  MapMode = 5
  Support = -> [XY_Plane662]
  sketch-geometry (9):
    g0: ArcOfCircle CenterX=0 CenterY=0 CenterZ=0 NormalX=0 NormalY=0 NormalZ=1 AngleXU=0 Radius=16.5 StartAngle=2.61799 EndAngle=5.75959
    g1: LineSegment StartX=-14.2894 StartY=8.25 StartZ=0 EndX=-1.3577 EndY=30.6484 EndZ=0
    g2: ArcOfCircle CenterX=23.5 CenterY=16.2968 CenterZ=0 NormalX=0 NormalY=0 NormalZ=1 AngleXU=0 Radius=28.7032 StartAngle=1.5708 EndAngle=2.61799
    g3: LineSegment StartX=23.5 StartY=45 StartZ=0 EndX=40 EndY=45 EndZ=0
    g4: LineSegment StartX=40 StartY=45 StartZ=0 EndX=40 EndY=15 EndZ=0
    g5: LineSegment StartX=40 StartY=15 StartZ=0 EndX=28.6962 EndY=15 EndZ=0
    g6: ArcOfCircle CenterX=28.6962 CenterY=13.2968 CenterZ=0 NormalX=0 NormalY=0 NormalZ=1 AngleXU=0 Radius=1.70319 StartAngle=1.5708 EndAngle=2.61799
    g7: LineSegment StartX=27.2211 StartY=14.1484 StartZ=0 EndX=14.2894 EndY=-8.25 EndZ=0
    g8: LineSegment [constr] StartX=-1.3577 StartY=30.6484 StartZ=0 EndX=27.2211 EndY=14.1484 EndZ=0
  constraints (21):
    c: Tangent(g0,g1) = 1.5708
    c: Tangent(g1,g2) = 1.5708
    c: Tangent(g2,g3) = 1.5708
    c: Perpendicular(g3,g4) = 4.71239
    c: Coincident(g4,g5)
    c: Horizontal(g5)
    c: Tangent(g5,g6) = -1.5708
    c: Tangent(g6,g7) = -1.5708
    c: Parallel(g7,g1)
    c: Radius(g0) = 16.5
    c: Horizontal(g3)
    c: DistanceY(g4,g4) = 30
    c: Tangent(g7,g0) = 1.5708
    c: DistanceX(g0,g4) = 40
    c: Coincident(g8,g1)
    c: Coincident(g8,g6)
    c: Perpendicular(g1,g8)
    c: DistanceX(g3,g3) = 16.5
    c: DistanceY(g0,g4) = 15
    c: Angle(g8) = -0.523599
    c: Coincident(g0,g-1)
FEATURE [Sketcher::SketchObject] Sketch1732
  MapMode = 5
  Support = -> [XY_Plane649]
  sketch-geometry (8):
    g0: LineSegment StartX=0 StartY=2.3094 StartZ=0 EndX=-2 EndY=1.1547 EndZ=0
    g1: LineSegment StartX=-2 StartY=1.1547 StartZ=0 EndX=-2 EndY=-1.1547 EndZ=0
    g2: LineSegment StartX=-2 StartY=-1.1547 StartZ=0 EndX=-2e-16 EndY=-2.3094 EndZ=0
    g3: LineSegment StartX=-2e-16 StartY=-2.3094 StartZ=0 EndX=2 EndY=-1.1547 EndZ=0
    g4: LineSegment StartX=2 StartY=-1.1547 StartZ=0 EndX=2 EndY=1.1547 EndZ=0
    g5: LineSegment StartX=2 StartY=1.1547 StartZ=0 EndX=0 EndY=2.3094 EndZ=0
    g6: Circle [constr] CenterX=0 CenterY=0 CenterZ=0 NormalX=0 NormalY=0 NormalZ=1 AngleXU=0 Radius=2.3094
    g7: Circle CenterX=0 CenterY=0 CenterZ=0 NormalX=0 NormalY=0 NormalZ=1 AngleXU=0 Radius=1
  constraints (18):
    c: Coincident(g0,g1)
    c: Coincident(g1,g2)
    c: Coincident(g2,g3)
    c: Coincident(g3,g4)
    c: Coincident(g4,g5)
    c: Coincident(g5,g0)
    c: Equal(g0, g1-g5) x5
    c: PointOnObject(g0,g6)
    c: PointOnObject(g1,g6)
    c: PointOnObject(g2,g6)
    c: PointOnObject(g3,g6)
    c: PointOnObject(g4,g6)
    c: PointOnObject(g5,g6)
    c: Coincident(g6,g-1)
    c: PointOnObject(g5,g-2)
    c: DistanceX(g0,g4) = 4
    c: Coincident(g7,g-1)
    c: Radius(g7) = 1
FEATURE [Sketcher::SketchObject] Sketch1733
  MapMode = 5
  Support = -> [XY_Plane681]
  sketch-geometry (1):
    g0: Circle CenterX=0 CenterY=0 CenterZ=0 NormalX=0 NormalY=0 NormalZ=1 AngleXU=0 Radius=1.9
  constraints (2):
    c: Coincident(g0,g-1)
    c: Radius(g0) = 1.9
FEATURE [Sketcher::SketchObject] Sketch1735
  MapMode = 5
  Support = -> [XY_Plane654]
FEATURE [Sketcher::SketchObject] Sketch1736
  MapMode = 5
  Support = -> [XY_Plane660]
FEATURE [Sketcher::SketchObject] Sketch1739
  MapMode = 5
  Support = -> [XY_Plane648]
FEATURE [Sketcher::SketchObject] Sketch1742
  MapMode = 5
  Support = -> [XY_Plane661]
  sketch-geometry (1):
    g0: Circle CenterX=0 CenterY=0 CenterZ=0 NormalX=0 NormalY=0 NormalZ=1 AngleXU=0 Radius=1.9
  constraints (2):
    c: Coincident(g0,g-1)
    c: Radius(g0) = 1.9
FEATURE [Sketcher::SketchObject] Sketch1743
  MapMode = 5
  Support = -> [XY_Plane651]
  sketch-geometry (8):
    g0: LineSegment StartX=0 StartY=2.3094 StartZ=0 EndX=-2 EndY=1.1547 EndZ=0
    g1: LineSegment StartX=-2 StartY=1.1547 StartZ=0 EndX=-2 EndY=-1.1547 EndZ=0
    g2: LineSegment StartX=-2 StartY=-1.1547 StartZ=0 EndX=-2e-16 EndY=-2.3094 EndZ=0
    g3: LineSegment StartX=-2e-16 StartY=-2.3094 StartZ=0 EndX=2 EndY=-1.1547 EndZ=0
    g4: LineSegment StartX=2 StartY=-1.1547 StartZ=0 EndX=2 EndY=1.1547 EndZ=0
    g5: LineSegment StartX=2 StartY=1.1547 StartZ=0 EndX=0 EndY=2.3094 EndZ=0
    g6: Circle [constr] CenterX=0 CenterY=0 CenterZ=0 NormalX=0 NormalY=0 NormalZ=1 AngleXU=0 Radius=2.3094
    g7: Circle CenterX=0 CenterY=0 CenterZ=0 NormalX=0 NormalY=0 NormalZ=1 AngleXU=0 Radius=1
  constraints (18):
    c: Coincident(g0,g1)
    c: Coincident(g1,g2)
    c: Coincident(g2,g3)
    c: Coincident(g3,g4)
    c: Coincident(g4,g5)
    c: Coincident(g5,g0)
    c: Equal(g0, g1-g5) x5
    c: PointOnObject(g0,g6)
    c: PointOnObject(g1,g6)
    c: PointOnObject(g2,g6)
    c: PointOnObject(g3,g6)
    c: PointOnObject(g4,g6)
    c: PointOnObject(g5,g6)
    c: Coincident(g6,g-1)
    c: PointOnObject(g5,g-2)
    c: DistanceX(g0,g4) = 4
    c: Coincident(g7,g-1)
    c: Radius(g7) = 1
FEATURE [Sketcher::SketchObject] Sketch1744
  MapMode = 5
  Support = -> [XY_Plane609]
  sketch-geometry (2):
    g0: Circle CenterX=0 CenterY=0 CenterZ=0 NormalX=0 NormalY=0 NormalZ=1 AngleXU=0 Radius=4
    g1: Circle CenterX=0 CenterY=0 CenterZ=0 NormalX=0 NormalY=0 NormalZ=1 AngleXU=0 Radius=6.25
  constraints (4):
    c: Coincident(g0,g-1)
    c: Coincident(g1,g0)
    c: Radius(g0) = 4
    c: Radius(g1) = 6.25
FEATURE [Sketcher::SketchObject] Sketch1747
  MapMode = 5
  Support = -> [XY_Plane658]
  sketch-geometry (8):
    g0: LineSegment StartX=0 StartY=3.17543 StartZ=0 EndX=-2.75 EndY=1.58771 EndZ=0
    g1: LineSegment StartX=-2.75 StartY=1.58771 StartZ=0 EndX=-2.75 EndY=-1.58771 EndZ=0
    g2: LineSegment StartX=-2.75 StartY=-1.58771 StartZ=0 EndX=0 EndY=-3.17543 EndZ=0
    g3: LineSegment StartX=0 StartY=-3.17543 StartZ=0 EndX=2.75 EndY=-1.58771 EndZ=0
    g4: LineSegment StartX=2.75 StartY=-1.58771 StartZ=0 EndX=2.75 EndY=1.58771 EndZ=0
    g5: LineSegment StartX=2.75 StartY=1.58771 StartZ=0 EndX=0 EndY=3.17543 EndZ=0
    g6: Circle [constr] CenterX=0 CenterY=0 CenterZ=0 NormalX=0 NormalY=0 NormalZ=1 AngleXU=0 Radius=3.17543
    g7: Circle CenterX=0 CenterY=0 CenterZ=0 NormalX=0 NormalY=0 NormalZ=1 AngleXU=0 Radius=1.5
  constraints (18):
    c: Coincident(g0,g1)
    c: Coincident(g1,g2)
    c: Coincident(g2,g3)
    c: Coincident(g3,g4)
    c: Coincident(g4,g5)
    c: Coincident(g5,g0)
    c: Equal(g0, g1-g5) x5
    c: PointOnObject(g0,g6)
    c: PointOnObject(g1,g6)
    c: PointOnObject(g2,g6)
    c: PointOnObject(g3,g6)
    c: PointOnObject(g4,g6)
    c: PointOnObject(g5,g6)
    c: Coincident(g6,g-1)
    c: PointOnObject(g5,g-2)
    c: DistanceX(g0,g4) = 5.5
    c: Coincident(g7,g-1)
    c: Radius(g7) = 1.5
FEATURE [Sketcher::SketchObject] Sketch1749
  MapMode = 5
  Support = -> [XY_Plane606]
  sketch-geometry (8):
    g0: LineSegment StartX=0 StartY=3.17543 StartZ=0 EndX=-2.75 EndY=1.58771 EndZ=0
    g1: LineSegment StartX=-2.75 StartY=1.58771 StartZ=0 EndX=-2.75 EndY=-1.58771 EndZ=0
    g2: LineSegment StartX=-2.75 StartY=-1.58771 StartZ=0 EndX=0 EndY=-3.17543 EndZ=0
    g3: LineSegment StartX=0 StartY=-3.17543 StartZ=0 EndX=2.75 EndY=-1.58771 EndZ=0
    g4: LineSegment StartX=2.75 StartY=-1.58771 StartZ=0 EndX=2.75 EndY=1.58771 EndZ=0
    g5: LineSegment StartX=2.75 StartY=1.58771 StartZ=0 EndX=0 EndY=3.17543 EndZ=0
    g6: Circle [constr] CenterX=0 CenterY=0 CenterZ=0 NormalX=0 NormalY=0 NormalZ=1 AngleXU=0 Radius=3.17543
    g7: Circle CenterX=0 CenterY=0 CenterZ=0 NormalX=0 NormalY=0 NormalZ=1 AngleXU=0 Radius=1.5
  constraints (18):
    c: Coincident(g0,g1)
    c: Coincident(g1,g2)
    c: Coincident(g2,g3)
    c: Coincident(g3,g4)
    c: Coincident(g4,g5)
    c: Coincident(g5,g0)
    c: Equal(g0, g1-g5) x5
    c: PointOnObject(g0,g6)
    c: PointOnObject(g1,g6)
    c: PointOnObject(g2,g6)
    c: PointOnObject(g3,g6)
    c: PointOnObject(g4,g6)
    c: PointOnObject(g5,g6)
    c: Coincident(g6,g-1)
    c: PointOnObject(g5,g-2)
    c: DistanceX(g0,g4) = 5.5
    c: Coincident(g7,g-1)
    c: Radius(g7) = 1.5
FEATURE [Sketcher::SketchObject] Sketch1755
  MapMode = 5
  Placement = pos=(0,0,0) rot=(0.57735,0.57735,0.57735;2.0944rad)
  Support = -> [YZ_Plane596]
  sketch-geometry (4):
    g0: LineSegment StartX=18.5 StartY=7.1 StartZ=0 EndX=21.5 EndY=7.1 EndZ=0
    g1: LineSegment StartX=21.5 StartY=7.1 StartZ=0 EndX=21.5 EndY=12.9 EndZ=0
    g2: LineSegment StartX=21.5 StartY=12.9 StartZ=0 EndX=18.5 EndY=12.9 EndZ=0
    g3: LineSegment StartX=18.5 StartY=12.9 StartZ=0 EndX=18.5 EndY=7.1 EndZ=0
  constraints (12):
    c: Coincident(g0,g1)
    c: Coincident(g1,g2)
    c: Coincident(g2,g3)
    c: Coincident(g3,g0)
    c: Horizontal(g0)
    c: Horizontal(g2)
    c: Vertical(g1)
    c: Vertical(g3)
    c: DistanceX(g2,g2) = 3
    c: DistanceY(g1,g1) = 5.8
    c: DistanceY(g-1,g0) = 7.1
    c: DistanceX(g-1,g0) = 21.5
FEATURE [Sketcher::SketchObject] Sketch1761
  MapMode = 5
  Placement = pos=(0,0,0) rot=(1,0,0;1.5708rad)
  Support = -> [XZ_Plane692]
  sketch-geometry (8):
    g0: LineSegment StartX=-1.5 StartY=2.25 StartZ=0 EndX=-3.25 EndY=2.25 EndZ=0
    g1: LineSegment StartX=-3.25 StartY=2.25 StartZ=0 EndX=-3.25 EndY=1.25 EndZ=0
    g2: LineSegment StartX=-3.25 StartY=1.25 StartZ=0 EndX=-2 EndY=1.25 EndZ=0
    g3: LineSegment StartX=-2 StartY=1.25 StartZ=0 EndX=-2 EndY=-1.25 EndZ=0
    g4: LineSegment StartX=-2 StartY=-1.25 StartZ=0 EndX=-3.25 EndY=-1.25 EndZ=0
    g5: LineSegment StartX=-3.25 StartY=-1.25 StartZ=0 EndX=-3.25 EndY=-2.25 EndZ=0
    g6: LineSegment StartX=-3.25 StartY=-2.25 StartZ=0 EndX=-1.5 EndY=-2.25 EndZ=0
    g7: LineSegment StartX=-1.5 StartY=-2.25 StartZ=0 EndX=-1.5 EndY=2.25 EndZ=0
  constraints (23):
    c: Horizontal(g0)
    c: Coincident(g0,g1)
    c: Vertical(g1)
    c: Coincident(g1,g2)
    c: Horizontal(g2)
    c: Coincident(g2,g3)
    c: Vertical(g3)
    c: Coincident(g3,g4)
    c: Horizontal(g4)
    c: Coincident(g4,g5)
    c: Vertical(g5)
    c: Coincident(g5,g6)
    c: Horizontal(g6)
    c: Coincident(g6,g7)
    c: Vertical(g7)
    c: Coincident(g0,g7)
    c: Equal(g1,g5)
    c: Symmetric(g4,g1,g-1)
    c: DistanceX(g0,g-1) = 1.5
    c: DistanceY(g3,g3) = 2.5
    c: DistanceY(g7,g7) = 4.5
    c: DistanceX(g0,g-1) = 3.25
    c: DistanceX(g2,g-1) = 2
FEATURE [Sketcher::SketchObject] Sketch1762
  MapMode = 5
  Placement = pos=(0,0,0) rot=(1,0,0;1.5708rad)
  Support = -> [XZ_Plane640]
  sketch-geometry (8):
    g0: LineSegment StartX=-1.5 StartY=2.25 StartZ=0 EndX=-3.25 EndY=2.25 EndZ=0
    g1: LineSegment StartX=-3.25 StartY=2.25 StartZ=0 EndX=-3.25 EndY=1.25 EndZ=0
    g2: LineSegment StartX=-3.25 StartY=1.25 StartZ=0 EndX=-2 EndY=1.25 EndZ=0
    g3: LineSegment StartX=-2 StartY=1.25 StartZ=0 EndX=-2 EndY=-1.25 EndZ=0
    g4: LineSegment StartX=-2 StartY=-1.25 StartZ=0 EndX=-3.25 EndY=-1.25 EndZ=0
    g5: LineSegment StartX=-3.25 StartY=-1.25 StartZ=0 EndX=-3.25 EndY=-2.25 EndZ=0
    g6: LineSegment StartX=-3.25 StartY=-2.25 StartZ=0 EndX=-1.5 EndY=-2.25 EndZ=0
    g7: LineSegment StartX=-1.5 StartY=-2.25 StartZ=0 EndX=-1.5 EndY=2.25 EndZ=0
  constraints (23):
    c: Horizontal(g0)
    c: Coincident(g0,g1)
    c: Vertical(g1)
    c: Coincident(g1,g2)
    c: Horizontal(g2)
    c: Coincident(g2,g3)
    c: Vertical(g3)
    c: Coincident(g3,g4)
    c: Horizontal(g4)
    c: Coincident(g4,g5)
    c: Vertical(g5)
    c: Coincident(g5,g6)
    c: Horizontal(g6)
    c: Coincident(g6,g7)
    c: Vertical(g7)
    c: Coincident(g0,g7)
    c: Equal(g1,g5)
    c: Symmetric(g4,g1,g-1)
    c: DistanceX(g0,g-1) = 1.5
    c: DistanceY(g3,g3) = 2.5
    c: DistanceY(g7,g7) = 4.5
    c: DistanceX(g0,g-1) = 3.25
    c: DistanceX(g2,g-1) = 2
FEATURE [Sketcher::SketchObject] Sketch1766
  MapMode = 5
  Placement = pos=(0,0,0) rot=(1,0,0;1.5708rad)
  Support = -> [XZ_Plane638]
  sketch-geometry (8):
    g0: LineSegment StartX=-1.5 StartY=2.25 StartZ=0 EndX=-3.25 EndY=2.25 EndZ=0
    g1: LineSegment StartX=-3.25 StartY=2.25 StartZ=0 EndX=-3.25 EndY=1.25 EndZ=0
    g2: LineSegment StartX=-3.25 StartY=1.25 StartZ=0 EndX=-2 EndY=1.25 EndZ=0
    g3: LineSegment StartX=-2 StartY=1.25 StartZ=0 EndX=-2 EndY=-1.25 EndZ=0
    g4: LineSegment StartX=-2 StartY=-1.25 StartZ=0 EndX=-3.25 EndY=-1.25 EndZ=0
    g5: LineSegment StartX=-3.25 StartY=-1.25 StartZ=0 EndX=-3.25 EndY=-2.25 EndZ=0
    g6: LineSegment StartX=-3.25 StartY=-2.25 StartZ=0 EndX=-1.5 EndY=-2.25 EndZ=0
    g7: LineSegment StartX=-1.5 StartY=-2.25 StartZ=0 EndX=-1.5 EndY=2.25 EndZ=0
  constraints (23):
    c: Horizontal(g0)
    c: Coincident(g0,g1)
    c: Vertical(g1)
    c: Coincident(g1,g2)
    c: Horizontal(g2)
    c: Coincident(g2,g3)
    c: Vertical(g3)
    c: Coincident(g3,g4)
    c: Horizontal(g4)
    c: Coincident(g4,g5)
    c: Vertical(g5)
    c: Coincident(g5,g6)
    c: Horizontal(g6)
    c: Coincident(g6,g7)
    c: Vertical(g7)
    c: Coincident(g0,g7)
    c: Equal(g1,g5)
    c: Symmetric(g4,g1,g-1)
    c: DistanceX(g0,g-1) = 1.5
    c: DistanceY(g3,g3) = 2.5
    c: DistanceY(g7,g7) = 4.5
    c: DistanceX(g0,g-1) = 3.25
    c: DistanceX(g2,g-1) = 2
FEATURE [PartDesign::Pad] Pad653  label="M3x20 Head056"
  Length = 3
  Length2 = 100
  Profile = -> Sketch1653
  Type = 0
FEATURE [Sketcher::SketchObject] Sketch1658
  MapMode = 5
  Placement = pos=(0,0,3) rot=(0,0,1;0rad)
  Support = -> [Pad653]
  sketch-geometry (1):
    g0: Circle CenterX=0 CenterY=0 CenterZ=0 NormalX=0 NormalY=0 NormalZ=1 AngleXU=0 Radius=1.5
  constraints (2):
    c: Coincident(g0,g-1)
    c: Radius(g0) = 1.5
FEATURE [PartDesign::Pad] Pad654  label="M3 Nut Primitive128"
  Length = 1.2
  Length2 = 1.2
  Profile = -> Sketch1629
  Type = 4
FEATURE [Sketcher::SketchObject] Sketch1619
  ExternalGeometry = -> [Pad654]
  MapMode = 5
  Placement = pos=(0,0,0) rot=(0.57735,0.57735,0.57735;2.0944rad)
  Support = -> [YZ_Plane601]
  sketch-geometry (6):
    g0: LineSegment StartX=-2.67543 StartY=1.2 StartZ=0 EndX=-3.67543 EndY=1.2 EndZ=0
    g1: LineSegment StartX=-3.67543 StartY=1.2 StartZ=0 EndX=-3.67543 EndY=-1.2 EndZ=0
    g2: LineSegment StartX=-3.67543 StartY=-1.2 StartZ=0 EndX=-2.67543 EndY=-1.2 EndZ=0
    g3: LineSegment StartX=-2.67543 StartY=-1.2 StartZ=0 EndX=-3.17543 EndY=-1 EndZ=0
    g4: LineSegment StartX=-3.17543 StartY=-1 StartZ=0 EndX=-3.17543 EndY=1 EndZ=0
    g5: LineSegment StartX=-3.17543 StartY=1 StartZ=0 EndX=-2.67543 EndY=1.2 EndZ=0
  constraints (15):
    c: Horizontal(g0)
    c: Coincident(g0,g1)
    c: Coincident(g1,g2)
    c: Coincident(g2,g3)
    c: Coincident(g3,g4)
    c: Coincident(g4,g5)
    c: Coincident(g5,g0)
    c: Symmetric(g4,g3,g-1)
    c: Symmetric(g0,g2,g-1)
    c: Symmetric(g1,g0,g-1)
    c: DistanceX(g0,g4) = 0.5
    c: DistanceY(g3,g4) = 2
    c: DistanceY(g1,g0) = 2.4
    c: PointOnObject(g3,g-3)
    c: DistanceX(g4,g0) = 0.5
FEATURE [PartDesign::Groove] Groove136  label="M3 Nut Smooth130"
  Angle = 360
  Axis = (-2e-16,3e-16,1)
  Base = (0,0,0)
  BaseFeature = -> Pad654
  Profile = -> Sketch1619
  ReferenceAxis = -> Sketch1619 [V_Axis]
  Reversed = true
FEATURE [PartDesign::Chamfer] Chamfer352  label="M3 Nut Smooth Hole149"
  Base = -> Groove136 [Edge24,Edge23]
  BaseFeature = -> Groove136
  Size = 0.2
FEATURE [PartDesign::Pad] Pad686  label="M3 Nut Primitive132"
  Length = 0.6
  Length2 = 0.6
  Profile = -> Sketch1732
  Type = 4
FEATURE [Sketcher::SketchObject] Sketch1717
  ExternalGeometry = -> [Pad686]
  MapMode = 5
  Placement = pos=(0,0,0) rot=(0.57735,0.57735,0.57735;2.0944rad)
  Support = -> [YZ_Plane652]
  sketch-geometry (6):
    g0: LineSegment StartX=-1.9594 StartY=0.6 StartZ=0 EndX=-2.8094 EndY=0.6 EndZ=0
    g1: LineSegment StartX=-2.8094 StartY=0.6 StartZ=0 EndX=-2.8094 EndY=-0.6 EndZ=0
    g2: LineSegment StartX=-2.8094 StartY=-0.6 StartZ=0 EndX=-1.9594 EndY=-0.6 EndZ=0
    g3: LineSegment StartX=-1.9594 StartY=-0.6 StartZ=0 EndX=-2.3094 EndY=-0.4 EndZ=0
    g4: LineSegment StartX=-2.3094 StartY=-0.4 StartZ=0 EndX=-2.3094 EndY=0.4 EndZ=0
    g5: LineSegment StartX=-2.3094 StartY=0.4 StartZ=0 EndX=-1.9594 EndY=0.6 EndZ=0
  constraints (15):
    c: Horizontal(g0)
    c: Coincident(g0,g1)
    c: Coincident(g1,g2)
    c: Coincident(g2,g3)
    c: Coincident(g3,g4)
    c: Coincident(g4,g5)
    c: Coincident(g5,g0)
    c: Symmetric(g4,g3,g-1)
    c: Symmetric(g0,g2,g-1)
    c: Symmetric(g1,g0,g-1)
    c: DistanceX(g0,g4) = 0.5
    c: DistanceY(g3,g4) = 0.8
    c: DistanceY(g1,g0) = 1.2
    c: PointOnObject(g3,g-3)
    c: DistanceX(g4,g0) = 0.35
FEATURE [PartDesign::Pad] Pad687  label="M3x8 Head087"
  Length = 2
  Length2 = 100
  Profile = -> Sketch1671
  Type = 0
FEATURE [Sketcher::SketchObject] Sketch1669
  MapMode = 5
  Placement = pos=(0,0,2) rot=(0,0,1;0rad)
  Support = -> [Pad687]
  sketch-geometry (1):
    g0: Circle CenterX=0 CenterY=0 CenterZ=0 NormalX=0 NormalY=0 NormalZ=1 AngleXU=0 Radius=1
  constraints (2):
    c: Coincident(g0,g-1)
    c: Radius(g0) = 1
FEATURE [PartDesign::Pad] Pad688  label="M3 Nut Primitive133"
  Length = 1.2
  Length2 = 1.2
  Profile = -> Sketch1602
  Type = 4
FEATURE [Sketcher::SketchObject] Sketch1612
  ExternalGeometry = -> [Pad688]
  MapMode = 5
  Placement = pos=(0,0,0) rot=(0.57735,0.57735,0.57735;2.0944rad)
  Support = -> [YZ_Plane580]
  sketch-geometry (6):
    g0: LineSegment StartX=-2.67543 StartY=1.2 StartZ=0 EndX=-3.67543 EndY=1.2 EndZ=0
    g1: LineSegment StartX=-3.67543 StartY=1.2 StartZ=0 EndX=-3.67543 EndY=-1.2 EndZ=0
    g2: LineSegment StartX=-3.67543 StartY=-1.2 StartZ=0 EndX=-2.67543 EndY=-1.2 EndZ=0
    g3: LineSegment StartX=-2.67543 StartY=-1.2 StartZ=0 EndX=-3.17543 EndY=-1 EndZ=0
    g4: LineSegment StartX=-3.17543 StartY=-1 StartZ=0 EndX=-3.17543 EndY=1 EndZ=0
    g5: LineSegment StartX=-3.17543 StartY=1 StartZ=0 EndX=-2.67543 EndY=1.2 EndZ=0
  constraints (15):
    c: Horizontal(g0)
    c: Coincident(g0,g1)
    c: Coincident(g1,g2)
    c: Coincident(g2,g3)
    c: Coincident(g3,g4)
    c: Coincident(g4,g5)
    c: Coincident(g5,g0)
    c: Symmetric(g4,g3,g-1)
    c: Symmetric(g0,g2,g-1)
    c: Symmetric(g1,g0,g-1)
    c: DistanceX(g0,g4) = 0.5
    c: DistanceY(g3,g4) = 2
    c: DistanceY(g1,g0) = 2.4
    c: PointOnObject(g3,g-3)
    c: DistanceX(g4,g0) = 0.5
FEATURE [PartDesign::Pad] Pad689  label="M3x8 Head088"
  Length = 2
  Length2 = 100
  Profile = -> Sketch1557
  Type = 0
FEATURE [Sketcher::SketchObject] Sketch1673
  MapMode = 5
  Placement = pos=(0,0,2) rot=(0,0,1;0rad)
  Support = -> [Pad689]
  sketch-geometry (1):
    g0: Circle CenterX=0 CenterY=0 CenterZ=0 NormalX=0 NormalY=0 NormalZ=1 AngleXU=0 Radius=1
  constraints (2):
    c: Coincident(g0,g-1)
    c: Radius(g0) = 1
FEATURE [PartDesign::Pad] Pad690  label="Baseblock014"
  Length = 15
  Length2 = 15
  Placement = pos=(0,0,0) rot=(1,0,0;1.5708rad)
  Profile = -> Sketch1599
  Type = 4
FEATURE [Sketcher::SketchObject] Sketch1589
  MapMode = 5
  Placement = pos=(0,0,-6.9576e-12) rot=(1,0,0;3.14159rad)
  Support = -> [Pad690]
  sketch-geometry (4):
    g0: ArcOfCircle CenterX=0 CenterY=0 CenterZ=0 NormalX=0 NormalY=0 NormalZ=1 AngleXU=0 Radius=20 StartAngle=2.29353 EndAngle=3.98965
    g1: LineSegment StartX=-13.2288 StartY=15 StartZ=0 EndX=-23.2288 EndY=15 EndZ=0
    g2: LineSegment StartX=-23.2288 StartY=15 StartZ=0 EndX=-23.2288 EndY=-15 EndZ=0
    g3: LineSegment StartX=-23.2288 StartY=-15 StartZ=0 EndX=-13.2288 EndY=-15 EndZ=0
  constraints (12):
    c: Coincident(g0,g-1)
    c: Vertical(g0,g0)
    c: Coincident(g0,g1)
    c: Coincident(g1,g2)
    c: Vertical(g2)
    c: Coincident(g2,g3)
    c: Coincident(g3,g0)
    c: Horizontal(g3)
    c: Radius(g0) = 20
    c: DistanceX(g1,g1) = 10
    c: DistanceY(g2,g2) = 30
    c: Horizontal(g1)
FEATURE [PartDesign::Groove] Groove141  label="Halfspherical Shape003"
  Angle = 360
  Axis = (0,-1,7e-16)
  Base = (0,0,-6.9577e-12)
  BaseFeature = -> Pad690
  Placement = pos=(0,0,0) rot=(1,0,0;1.5708rad)
  Profile = -> Sketch1589
  ReferenceAxis = -> Sketch1589 [V_Axis]
  Reversed = true
FEATURE [PartDesign::SubtractivePipe] SubtractivePipe018  label="Horizontal Profile003"
  AuxilleryCurvelinear = true
  AuxillerySpineTangent = false
  BaseFeature = -> Groove141
  Binormal = (0,0,0)
  Mode = 0
  Placement = pos=(0,0,0) rot=(1,0,0;1.5708rad)
  Profile = -> Sketch1682
  Spine = -> Groove141 [Edge2,Edge1]
  SpineTangent = false
  Transformation = 0
  Transition = 0
FEATURE [PartDesign::Pad] Pad691  label="M3 Nut Primitive134"
  Length = 1.2
  Length2 = 1.2
  Profile = -> Sketch1534
  Type = 4
FEATURE [Sketcher::SketchObject] Sketch1545
  ExternalGeometry = -> [Pad691]
  MapMode = 5
  Placement = pos=(0,0,0) rot=(0.57735,0.57735,0.57735;2.0944rad)
  Support = -> [YZ_Plane594]
  sketch-geometry (6):
    g0: LineSegment StartX=-2.67543 StartY=1.2 StartZ=0 EndX=-3.67543 EndY=1.2 EndZ=0
    g1: LineSegment StartX=-3.67543 StartY=1.2 StartZ=0 EndX=-3.67543 EndY=-1.2 EndZ=0
    g2: LineSegment StartX=-3.67543 StartY=-1.2 StartZ=0 EndX=-2.67543 EndY=-1.2 EndZ=0
    g3: LineSegment StartX=-2.67543 StartY=-1.2 StartZ=0 EndX=-3.17543 EndY=-1 EndZ=0
    g4: LineSegment StartX=-3.17543 StartY=-1 StartZ=0 EndX=-3.17543 EndY=1 EndZ=0
    g5: LineSegment StartX=-3.17543 StartY=1 StartZ=0 EndX=-2.67543 EndY=1.2 EndZ=0
  constraints (15):
    c: Horizontal(g0)
    c: Coincident(g0,g1)
    c: Coincident(g1,g2)
    c: Coincident(g2,g3)
    c: Coincident(g3,g4)
    c: Coincident(g4,g5)
    c: Coincident(g5,g0)
    c: Symmetric(g4,g3,g-1)
    c: Symmetric(g0,g2,g-1)
    c: Symmetric(g1,g0,g-1)
    c: DistanceX(g0,g4) = 0.5
    c: DistanceY(g3,g4) = 2
    c: DistanceY(g1,g0) = 2.4
    c: PointOnObject(g3,g-3)
    c: DistanceX(g4,g0) = 0.5
FEATURE [PartDesign::Pad] Pad692  label="M3 Nut Primitive135"
  Length = 0.6
  Length2 = 0.6
  Profile = -> Sketch1672
  Type = 4
FEATURE [Sketcher::SketchObject] Sketch1724
  ExternalGeometry = -> [Pad692]
  MapMode = 5
  Placement = pos=(0,0,0) rot=(0.57735,0.57735,0.57735;2.0944rad)
  Support = -> [YZ_Plane665]
  sketch-geometry (6):
    g0: LineSegment StartX=-1.9594 StartY=0.6 StartZ=0 EndX=-2.8094 EndY=0.6 EndZ=0
    g1: LineSegment StartX=-2.8094 StartY=0.6 StartZ=0 EndX=-2.8094 EndY=-0.6 EndZ=0
    g2: LineSegment StartX=-2.8094 StartY=-0.6 StartZ=0 EndX=-1.9594 EndY=-0.6 EndZ=0
    g3: LineSegment StartX=-1.9594 StartY=-0.6 StartZ=0 EndX=-2.3094 EndY=-0.4 EndZ=0
    g4: LineSegment StartX=-2.3094 StartY=-0.4 StartZ=0 EndX=-2.3094 EndY=0.4 EndZ=0
    g5: LineSegment StartX=-2.3094 StartY=0.4 StartZ=0 EndX=-1.9594 EndY=0.6 EndZ=0
  constraints (15):
    c: Horizontal(g0)
    c: Coincident(g0,g1)
    c: Coincident(g1,g2)
    c: Coincident(g2,g3)
    c: Coincident(g3,g4)
    c: Coincident(g4,g5)
    c: Coincident(g5,g0)
    c: Symmetric(g4,g3,g-1)
    c: Symmetric(g0,g2,g-1)
    c: Symmetric(g1,g0,g-1)
    c: DistanceX(g0,g4) = 0.5
    c: DistanceY(g3,g4) = 0.8
    c: DistanceY(g1,g0) = 1.2
    c: PointOnObject(g3,g-3)
    c: DistanceX(g4,g0) = 0.35
FEATURE [PartDesign::Groove] Groove142  label="M3 Nut Smooth135"
  Angle = 360
  Axis = (-2e-16,3e-16,1)
  Base = (0,0,0)
  BaseFeature = -> Pad692
  Profile = -> Sketch1724
  ReferenceAxis = -> Sketch1724 [V_Axis]
  Reversed = true
FEATURE [PartDesign::Chamfer] Chamfer318  label="M3 Nut Smooth Hole134"
  Base = -> Groove142 [Edge24,Edge23]
  BaseFeature = -> Groove142
  Size = 0.2
FEATURE [PartDesign::Pad] Pad693  label="M3x8 Head089"
  Length = 2
  Length2 = 100
  Profile = -> Sketch1624
  Type = 0
FEATURE [PartDesign::Pad] Pad694  label="M3x8 Thread085"
  BaseFeature = -> Pad689
  Length = 8
  Length2 = 100
  Profile = -> Sketch1673
  Type = 0
FEATURE [Sketcher::SketchObject] Sketch1675
  MapMode = 5
  Placement = pos=(0,0,0) rot=(1,0,0;3.14159rad)
  Support = -> [Pad694]
  sketch-geometry (7):
    g0: LineSegment StartX=0.77 StartY=0.44456 StartZ=0 EndX=0 EndY=0.889119 EndZ=0
    g1: LineSegment StartX=0 StartY=0.889119 StartZ=0 EndX=-0.77 EndY=0.44456 EndZ=0
    g2: LineSegment StartX=-0.77 StartY=0.44456 StartZ=0 EndX=-0.77 EndY=-0.44456 EndZ=0
    g3: LineSegment StartX=-0.77 StartY=-0.44456 StartZ=0 EndX=3.85628e-11 EndY=-0.889119 EndZ=0
    g4: LineSegment StartX=3.85628e-11 StartY=-0.889119 StartZ=0 EndX=0.77 EndY=-0.44456 EndZ=0
    g5: LineSegment StartX=0.77 StartY=-0.44456 StartZ=0 EndX=0.77 EndY=0.44456 EndZ=0
    g6: Circle [constr] CenterX=0 CenterY=0 CenterZ=0 NormalX=0 NormalY=0 NormalZ=1 AngleXU=0 Radius=0.889119
  constraints (16):
    c: Coincident(g0,g1)
    c: Coincident(g1,g2)
    c: Coincident(g2,g3)
    c: Coincident(g3,g4)
    c: Coincident(g4,g5)
    c: Coincident(g5,g0)
    c: Equal(g0, g1-g5) x5
    c: PointOnObject(g0,g6)
    c: PointOnObject(g1,g6)
    c: PointOnObject(g2,g6)
    c: PointOnObject(g3,g6)
    c: PointOnObject(g4,g6)
    c: PointOnObject(g5,g6)
    c: Coincident(g6,g-1)
    c: PointOnObject(g0,g-2)
    c: DistanceX(g1,g0) = 1.54
FEATURE [PartDesign::Pocket] Pocket595  label="M3x8 Wrench088"
  BaseFeature = -> Pad694
  Length = 1
  Length2 = 100
  Profile = -> Sketch1675
  Type = 0
FEATURE [PartDesign::Chamfer] Chamfer308  label="M3x8 Smooth079"
  Base = -> Pocket595 [Face11,Edge2,Edge24,Edge3]
  BaseFeature = -> Pocket595
  Size = 0.2
FEATURE [PartDesign::Pad] Pad695  label="M3x8 Head090"
  Length = 2
  Length2 = 100
  Profile = -> Sketch1733
  Type = 0
FEATURE [Sketcher::SketchObject] Sketch1729
  MapMode = 5
  Placement = pos=(0,0,2) rot=(0,0,1;0rad)
  Support = -> [Pad695]
  sketch-geometry (1):
    g0: Circle CenterX=0 CenterY=0 CenterZ=0 NormalX=0 NormalY=0 NormalZ=1 AngleXU=0 Radius=1
  constraints (2):
    c: Coincident(g0,g-1)
    c: Radius(g0) = 1
FEATURE [PartDesign::Pad] Pad697  label="M3 Nut Primitive136"
  Length = 1.2
  Length2 = 1.2
  Profile = -> Sketch1530
  Type = 4
FEATURE [Sketcher::SketchObject] Sketch1535
  ExternalGeometry = -> [Pad697]
  MapMode = 5
  Placement = pos=(0,0,0) rot=(0.57735,0.57735,0.57735;2.0944rad)
  Support = -> [YZ_Plane589]
  sketch-geometry (6):
    g0: LineSegment StartX=-2.67543 StartY=1.2 StartZ=0 EndX=-3.67543 EndY=1.2 EndZ=0
    g1: LineSegment StartX=-3.67543 StartY=1.2 StartZ=0 EndX=-3.67543 EndY=-1.2 EndZ=0
    g2: LineSegment StartX=-3.67543 StartY=-1.2 StartZ=0 EndX=-2.67543 EndY=-1.2 EndZ=0
    g3: LineSegment StartX=-2.67543 StartY=-1.2 StartZ=0 EndX=-3.17543 EndY=-1 EndZ=0
    g4: LineSegment StartX=-3.17543 StartY=-1 StartZ=0 EndX=-3.17543 EndY=1 EndZ=0
    g5: LineSegment StartX=-3.17543 StartY=1 StartZ=0 EndX=-2.67543 EndY=1.2 EndZ=0
  constraints (15):
    c: Horizontal(g0)
    c: Coincident(g0,g1)
    c: Coincident(g1,g2)
    c: Coincident(g2,g3)
    c: Coincident(g3,g4)
    c: Coincident(g4,g5)
    c: Coincident(g5,g0)
    c: Symmetric(g4,g3,g-1)
    c: Symmetric(g0,g2,g-1)
    c: Symmetric(g1,g0,g-1)
    c: DistanceX(g0,g4) = 0.5
    c: DistanceY(g3,g4) = 2
    c: DistanceY(g1,g0) = 2.4
    c: PointOnObject(g3,g-3)
    c: DistanceX(g4,g0) = 0.5
FEATURE [PartDesign::Groove] Groove145  label="M3 Nut Smooth137"
  Angle = 360
  Axis = (-2e-16,3e-16,1)
  Base = (0,0,0)
  BaseFeature = -> Pad697
  Profile = -> Sketch1535
  ReferenceAxis = -> Sketch1535 [V_Axis]
  Reversed = true
FEATURE [PartDesign::Chamfer] Chamfer311  label="M3 Nut Smooth Hole131"
  Base = -> Groove145 [Edge24,Edge23]
  BaseFeature = -> Groove145
  Size = 0.2
FEATURE [PartDesign::Pad] Pad698  label="Baseplate029"
  Length = 20
  Length2 = 100
  Profile = -> Sketch1585
  Type = 0
FEATURE [Sketcher::SketchObject] Sketch1596
  ExternalGeometry = -> [Pad698]
  MapMode = 5
  Placement = pos=(0,0,20) rot=(0,0,1;0rad)
  Support = -> [Pad698]
  sketch-geometry (18):
    g0: LineSegment StartX=-87.0711 StartY=22.0711 StartZ=0 EndX=-72.9287 EndY=7.92875 EndZ=0
    g1: LineSegment StartX=-50 StartY=17.1099 StartZ=0 EndX=-30 EndY=17.1099 EndZ=0
    g2: LineSegment StartX=-30 StartY=17.1099 StartZ=0 EndX=-30 EndY=25 EndZ=0
    g3: LineSegment StartX=-30 StartY=25 StartZ=0 EndX=-50 EndY=25 EndZ=0
    g4: LineSegment StartX=-50 StartY=25 StartZ=0 EndX=-50 EndY=17.1099 EndZ=0
    g5: LineSegment StartX=-55 StartY=25 StartZ=0 EndX=-55 EndY=17.1099 EndZ=0
    g6: LineSegment StartX=-55 StartY=25 StartZ=0 EndX=-80 EndY=25 EndZ=0
    g7: LineSegment StartX=-25 StartY=25 StartZ=0 EndX=-25 EndY=17.1099 EndZ=0
    g8: ArcOfCircle CenterX=-80 CenterY=15 CenterZ=0 NormalX=0 NormalY=0 NormalZ=1 AngleXU=0 Radius=10 StartAngle=1.5708 EndAngle=2.35619
    g9: ArcOfCircle CenterX=-50 CenterY=-14.75 CenterZ=0 NormalX=0 NormalY=0 NormalZ=1 AngleXU=0 Radius=32.2499 StartAngle=1.72646 EndAngle=2.36168
    g10: ArcOfCircle CenterX=-30 CenterY=-14.75 CenterZ=0 NormalX=0 NormalY=0 NormalZ=1 AngleXU=0 Radius=32.2499 StartAngle=0.781214 EndAngle=1.41513
    g11: ArcOfCircle CenterX=0 CenterY=15 CenterZ=0 NormalX=0 NormalY=0 NormalZ=1 AngleXU=0 Radius=10.0001 StartAngle=3.92281 EndAngle=4.1888
    g12: LineSegment StartX=-25 StartY=25 StartZ=0 EndX=-5 EndY=25 EndZ=0
    g13: LineSegment StartX=-5 StartY=25 StartZ=0 EndX=-5 EndY=6.33958 EndZ=0
    g14: LineSegment StartX=8 StartY=25 StartZ=0 EndX=48.5 EndY=25 EndZ=0
    g15: LineSegment StartX=48.5 StartY=25 StartZ=0 EndX=48.5 EndY=5 EndZ=0
    g16: LineSegment StartX=48.5 StartY=5 StartZ=0 EndX=8 EndY=5 EndZ=0
    g17: LineSegment StartX=8 StartY=5 StartZ=0 EndX=8 EndY=25 EndZ=0
  constraints (52):
    c: Coincident(g1,g2)
    c: Coincident(g2,g3)
    c: Coincident(g3,g4)
    c: Coincident(g4,g1)
    c: Horizontal(g1)
    c: Horizontal(g3)
    c: Vertical(g2)
    c: Vertical(g4)
    c: Coincident(g6,g5)
    c: Horizontal(g6)
    c: Vertical(g7)
    c: Vertical(g5)
    c: Coincident(g8,g0)
    c: Coincident(g9,g5)
    c: Coincident(g10,g7)
    c: Coincident(g12,g7)
    c: Horizontal(g12)
    c: Tangent(g8,g6) = -1.5708
    c: Horizontal(g5,g3)
    c: Horizontal(g2,g7)
    c: Horizontal(g1,g7)
    c: Horizontal(g5,g1)
    c: Tangent(g11,g10) = 1.5708
    c: Angle(g0) = -0.785398
    c: Radius(g8) = 10
    c: Coincident(g8,g-3)
    c: PointOnObject(g8,g0)
    c: Coincident(g9,g0)
    c: DistanceX(g5,g3) = 5
    c: DistanceX(g2,g7) = 5
    c: DistanceX(g11,g-1) = 5
    c: Coincident(g13,g12)
    c: Coincident(g13,g11)
    c: Vertical(g13)
    c: Coincident(g-4,g9)
    c: Coincident(g10,g-5)
    c: Distance(g0,g-4) = 5
    c: Coincident(g11,g-6)
    c: Vertical(g-4,g1)
    c: Vertical(g-5,g1)
    c: Coincident(g14,g15)
    c: Coincident(g15,g16)
    c: Coincident(g16,g17)
    c: Coincident(g17,g14)
    c: Horizontal(g14)
    c: Horizontal(g16)
    c: Vertical(g15)
    c: Vertical(g17)
    c: DistanceX(g-1,g16) = 8
    c: DistanceY(g-1,g16) = 5
    c: DistanceX(g14,g14) = 40.5
    c: DistanceY(g15,g15) = 20
FEATURE [PartDesign::Pad] Pad700  label="M3x20 Head061"
  Length = 3
  Length2 = 100
  Profile = -> Sketch1680
  Type = 0
FEATURE [Sketcher::SketchObject] Sketch1578
  MapMode = 5
  Placement = pos=(0,0,3) rot=(0,0,1;0rad)
  Support = -> [Pad700]
  sketch-geometry (1):
    g0: Circle CenterX=0 CenterY=0 CenterZ=0 NormalX=0 NormalY=0 NormalZ=1 AngleXU=0 Radius=1.5
  constraints (2):
    c: Coincident(g0,g-1)
    c: Radius(g0) = 1.5
FEATURE [PartDesign::Pad] Pad702  label="M3 Nut Primitive137"
  Length = 1.2
  Length2 = 1.2
  Profile = -> Sketch1618
  Type = 4
FEATURE [Sketcher::SketchObject] Sketch1600
  ExternalGeometry = -> [Pad702]
  MapMode = 5
  Placement = pos=(0,0,0) rot=(0.57735,0.57735,0.57735;2.0944rad)
  Support = -> [YZ_Plane577]
  sketch-geometry (6):
    g0: LineSegment StartX=-2.67543 StartY=1.2 StartZ=0 EndX=-3.67543 EndY=1.2 EndZ=0
    g1: LineSegment StartX=-3.67543 StartY=1.2 StartZ=0 EndX=-3.67543 EndY=-1.2 EndZ=0
    g2: LineSegment StartX=-3.67543 StartY=-1.2 StartZ=0 EndX=-2.67543 EndY=-1.2 EndZ=0
    g3: LineSegment StartX=-2.67543 StartY=-1.2 StartZ=0 EndX=-3.17543 EndY=-1 EndZ=0
    g4: LineSegment StartX=-3.17543 StartY=-1 StartZ=0 EndX=-3.17543 EndY=1 EndZ=0
    g5: LineSegment StartX=-3.17543 StartY=1 StartZ=0 EndX=-2.67543 EndY=1.2 EndZ=0
  constraints (15):
    c: Horizontal(g0)
    c: Coincident(g0,g1)
    c: Coincident(g1,g2)
    c: Coincident(g2,g3)
    c: Coincident(g3,g4)
    c: Coincident(g4,g5)
    c: Coincident(g5,g0)
    c: Symmetric(g4,g3,g-1)
    c: Symmetric(g0,g2,g-1)
    c: Symmetric(g1,g0,g-1)
    c: DistanceX(g0,g4) = 0.5
    c: DistanceY(g3,g4) = 2
    c: DistanceY(g1,g0) = 2.4
    c: PointOnObject(g3,g-3)
    c: DistanceX(g4,g0) = 0.5
FEATURE [PartDesign::Pad] Pad703
  Length = 10
  Length2 = 100
  Placement = pos=(0,0,0) rot=(1,0,0;1.5708rad)
  Profile = -> Sketch1552
  Reversed = true
  Type = 0
FEATURE [PartDesign::Pad] Pad704  label="M3 Nut Primitive138"
  Length = 0.6
  Length2 = 0.6
  Profile = -> Sketch1743
  Type = 4
FEATURE [Sketcher::SketchObject] Sketch1555
  ExternalGeometry = -> [Pad704]
  MapMode = 5
  Placement = pos=(0,0,0) rot=(0.57735,0.57735,0.57735;2.0944rad)
  Support = -> [YZ_Plane661]
  sketch-geometry (6):
    g0: LineSegment StartX=-1.9594 StartY=0.6 StartZ=0 EndX=-2.8094 EndY=0.6 EndZ=0
    g1: LineSegment StartX=-2.8094 StartY=0.6 StartZ=0 EndX=-2.8094 EndY=-0.6 EndZ=0
    g2: LineSegment StartX=-2.8094 StartY=-0.6 StartZ=0 EndX=-1.9594 EndY=-0.6 EndZ=0
    g3: LineSegment StartX=-1.9594 StartY=-0.6 StartZ=0 EndX=-2.3094 EndY=-0.4 EndZ=0
    g4: LineSegment StartX=-2.3094 StartY=-0.4 StartZ=0 EndX=-2.3094 EndY=0.4 EndZ=0
    g5: LineSegment StartX=-2.3094 StartY=0.4 StartZ=0 EndX=-1.9594 EndY=0.6 EndZ=0
  constraints (15):
    c: Horizontal(g0)
    c: Coincident(g0,g1)
    c: Coincident(g1,g2)
    c: Coincident(g2,g3)
    c: Coincident(g3,g4)
    c: Coincident(g4,g5)
    c: Coincident(g5,g0)
    c: Symmetric(g4,g3,g-1)
    c: Symmetric(g0,g2,g-1)
    c: Symmetric(g1,g0,g-1)
    c: DistanceX(g0,g4) = 0.5
    c: DistanceY(g3,g4) = 0.8
    c: DistanceY(g1,g0) = 1.2
    c: PointOnObject(g3,g-3)
    c: DistanceX(g4,g0) = 0.35
FEATURE [PartDesign::Groove] Groove140  label="M3 Nut Smooth134"
  Angle = 360
  Axis = (-2e-16,3e-16,1)
  Base = (0,0,0)
  BaseFeature = -> Pad704
  Profile = -> Sketch1555
  ReferenceAxis = -> Sketch1555 [V_Axis]
  Reversed = true
FEATURE [PartDesign::Chamfer] Chamfer327  label="M3 Nut Smooth Hole137"
  Base = -> Groove140 [Edge24,Edge23]
  BaseFeature = -> Groove140
  Size = 0.2
FEATURE [PartDesign::Pad] Pad706  label="M3 Nut Primitive139"
  Length = 1.2
  Length2 = 1.2
  Profile = -> Sketch1539
  Type = 4
FEATURE [Sketcher::SketchObject] Sketch1594
  ExternalGeometry = -> [Pad706]
  MapMode = 5
  Placement = pos=(0,0,0) rot=(0.57735,0.57735,0.57735;2.0944rad)
  Support = -> [YZ_Plane595]
  sketch-geometry (6):
    g0: LineSegment StartX=-2.67543 StartY=1.2 StartZ=0 EndX=-3.67543 EndY=1.2 EndZ=0
    g1: LineSegment StartX=-3.67543 StartY=1.2 StartZ=0 EndX=-3.67543 EndY=-1.2 EndZ=0
    g2: LineSegment StartX=-3.67543 StartY=-1.2 StartZ=0 EndX=-2.67543 EndY=-1.2 EndZ=0
    g3: LineSegment StartX=-2.67543 StartY=-1.2 StartZ=0 EndX=-3.17543 EndY=-1 EndZ=0
    g4: LineSegment StartX=-3.17543 StartY=-1 StartZ=0 EndX=-3.17543 EndY=1 EndZ=0
    g5: LineSegment StartX=-3.17543 StartY=1 StartZ=0 EndX=-2.67543 EndY=1.2 EndZ=0
  constraints (15):
    c: Horizontal(g0)
    c: Coincident(g0,g1)
    c: Coincident(g1,g2)
    c: Coincident(g2,g3)
    c: Coincident(g3,g4)
    c: Coincident(g4,g5)
    c: Coincident(g5,g0)
    c: Symmetric(g4,g3,g-1)
    c: Symmetric(g0,g2,g-1)
    c: Symmetric(g1,g0,g-1)
    c: DistanceX(g0,g4) = 0.5
    c: DistanceY(g3,g4) = 2
    c: DistanceY(g1,g0) = 2.4
    c: PointOnObject(g3,g-3)
    c: DistanceX(g4,g0) = 0.5
FEATURE [PartDesign::Pad] Pad707  label="M3 Nut Primitive140"
  Length = 0.6
  Length2 = 0.6
  Profile = -> Sketch1543
  Type = 4
FEATURE [PartDesign::Groove] Groove147  label="M3 Nut Smooth139"
  Angle = 360
  Axis = (-2e-16,3e-16,1)
  Base = (0,0,0)
  BaseFeature = -> Pad688
  Profile = -> Sketch1612
  ReferenceAxis = -> Sketch1612 [V_Axis]
  Reversed = true
FEATURE [PartDesign::Chamfer] Chamfer342  label="M3 Nut Smooth Hole143"
  Base = -> Groove147 [Edge24,Edge23]
  BaseFeature = -> Groove147
  Size = 0.2
FEATURE [PartDesign::Pad] Pad708  label="M3x20 Head062"
  Length = 3
  Length2 = 100
  Profile = -> Sketch1577
  Type = 0
FEATURE [Sketcher::SketchObject] Sketch1686
  MapMode = 5
  Placement = pos=(0,0,3) rot=(0,0,1;0rad)
  Support = -> [Pad708]
  sketch-geometry (1):
    g0: Circle CenterX=0 CenterY=0 CenterZ=0 NormalX=0 NormalY=0 NormalZ=1 AngleXU=0 Radius=1.5
  constraints (2):
    c: Coincident(g0,g-1)
    c: Radius(g0) = 1.5
FEATURE [PartDesign::Pad] Pad696  label="M3x20 Thread062"
  BaseFeature = -> Pad708
  Length = 20
  Length2 = 100
  Profile = -> Sketch1686
  Type = 0
FEATURE [Sketcher::SketchObject] Sketch1664
  MapMode = 5
  Placement = pos=(0,0,0) rot=(1,0,0;3.14159rad)
  Support = -> [Pad696]
  sketch-geometry (7):
    g0: LineSegment StartX=1.275 StartY=0.736122 StartZ=0 EndX=0 EndY=1.47224 EndZ=0
    g1: LineSegment StartX=0 StartY=1.47224 StartZ=0 EndX=-1.275 EndY=0.736122 EndZ=0
    g2: LineSegment StartX=-1.275 StartY=0.736122 StartZ=0 EndX=-1.275 EndY=-0.736122 EndZ=0
    g3: LineSegment StartX=-1.275 StartY=-0.736122 StartZ=0 EndX=1.34766e-11 EndY=-1.47224 EndZ=0
    g4: LineSegment StartX=1.34766e-11 StartY=-1.47224 StartZ=0 EndX=1.275 EndY=-0.736122 EndZ=0
    g5: LineSegment StartX=1.275 StartY=-0.736122 StartZ=0 EndX=1.275 EndY=0.736122 EndZ=0
    g6: Circle [constr] CenterX=0 CenterY=0 CenterZ=0 NormalX=0 NormalY=0 NormalZ=1 AngleXU=0 Radius=1.47224
  constraints (16):
    c: Coincident(g0,g1)
    c: Coincident(g1,g2)
    c: Coincident(g2,g3)
    c: Coincident(g3,g4)
    c: Coincident(g4,g5)
    c: Coincident(g5,g0)
    c: Equal(g0, g1-g5) x5
    c: PointOnObject(g0,g6)
    c: PointOnObject(g1,g6)
    c: PointOnObject(g2,g6)
    c: PointOnObject(g3,g6)
    c: PointOnObject(g4,g6)
    c: PointOnObject(g5,g6)
    c: Coincident(g6,g-1)
    c: PointOnObject(g0,g-2)
    c: DistanceX(g1,g0) = 2.55
FEATURE [PartDesign::Pocket] Pocket602  label="M3x20 Wrench062"
  BaseFeature = -> Pad696
  Length = 1.3
  Length2 = 100
  Profile = -> Sketch1664
  Type = 0
FEATURE [PartDesign::Chamfer] Chamfer304  label="M3x20 Smooth056"
  Base = -> Pocket602 [Face11,Edge2,Edge24,Edge3]
  BaseFeature = -> Pocket602
  Size = 0.2
FEATURE [PartDesign::Pad] Pad710  label="M3x8 Head091"
  Length = 3
  Length2 = 100
  Profile = -> Sketch1625
  Type = 0
FEATURE [Sketcher::SketchObject] Sketch1608
  MapMode = 5
  Placement = pos=(0,0,3) rot=(0,0,1;0rad)
  Support = -> [Pad710]
  sketch-geometry (1):
    g0: Circle CenterX=0 CenterY=0 CenterZ=0 NormalX=0 NormalY=0 NormalZ=1 AngleXU=0 Radius=1.5
  constraints (2):
    c: Coincident(g0,g-1)
    c: Radius(g0) = 1.5
FEATURE [PartDesign::Pad] Pad711  label="Ball Bearing Pin008"
  Length = 5
  Length2 = 100
  Profile = -> Sketch1570
  Type = 0
FEATURE [PartDesign::Chamfer] Chamfer315  label="Smooth Pinhead006"
  Base = -> Pad711 [Edge3]
  BaseFeature = -> Pad711
  Size = 0.4
FEATURE [PartDesign::Pad] Pad712  label="Baseplate030"
  Length = 25
  Length2 = 100
  Profile = -> Sketch1528
  Type = 0
FEATURE [Sketcher::SketchObject] Sketch1536
  MapMode = 5
  Placement = pos=(0,0,25) rot=(0,0,1;0rad)
  Support = -> [Pad712]
  sketch-geometry (4):
    g0: LineSegment StartX=8 StartY=0 StartZ=0 EndX=48.5 EndY=0 EndZ=0
    g1: LineSegment StartX=48.5 StartY=0 StartZ=0 EndX=48.5 EndY=-19 EndZ=0
    g2: LineSegment StartX=48.5 StartY=-19 StartZ=0 EndX=8 EndY=-19 EndZ=0
    g3: LineSegment StartX=8 StartY=-19 StartZ=0 EndX=8 EndY=0 EndZ=0
  constraints (12):
    c: Coincident(g0,g1)
    c: Coincident(g1,g2)
    c: Coincident(g2,g3)
    c: Coincident(g3,g0)
    c: Horizontal(g0)
    c: Horizontal(g2)
    c: Vertical(g1)
    c: Vertical(g3)
    c: PointOnObject(g0,g-1)
    c: DistanceY(g3,g3) = 19
    c: DistanceX(g0,g0) = 40.5
    c: DistanceX(g-1,g0) = 8
FEATURE [PartDesign::Pocket] Pocket606  label="Servopocket003"
  BaseFeature = -> Pad712
  Length = 20
  Length2 = 100
  Profile = -> Sketch1536
  Type = 0
FEATURE [PartDesign::Pad] Pad713  label="M3x20 Head063"
  Length = 3
  Length2 = 100
  Profile = -> Sketch1572
  Type = 0
FEATURE [Sketcher::SketchObject] Sketch1582
  MapMode = 5
  Placement = pos=(0,0,3) rot=(0,0,1;0rad)
  Support = -> [Pad713]
  sketch-geometry (1):
    g0: Circle CenterX=0 CenterY=0 CenterZ=0 NormalX=0 NormalY=0 NormalZ=1 AngleXU=0 Radius=1.5
  constraints (2):
    c: Coincident(g0,g-1)
    c: Radius(g0) = 1.5
FEATURE [PartDesign::Groove] Groove148  label="M3 Nut Smooth140"
  Angle = 360
  Axis = (-2e-16,3e-16,1)
  Base = (0,0,0)
  BaseFeature = -> Pad691
  Profile = -> Sketch1545
  ReferenceAxis = -> Sketch1545 [V_Axis]
  Reversed = true
FEATURE [PartDesign::Chamfer] Chamfer305  label="M3 Nut Smooth Hole129"
  Base = -> Groove148 [Edge24,Edge23]
  BaseFeature = -> Groove148
  Size = 0.2
FEATURE [PartDesign::Pocket] Pocket614  label="Leg and Servo Pockets003"
  BaseFeature = -> Pad698
  Length = 20
  Length2 = 100
  Profile = -> Sketch1596
  Type = 0
FEATURE [PartDesign::Fillet] Fillet206  label="Smooth Leg Pockets003"
  Base = -> Pocket614 [Edge76,Edge72,Edge73,Edge75,Edge69,Edge70,Edge71,Edge68,Edge77,Edge81,Edge79,Edge80]
  BaseFeature = -> Pocket614
  Radius = 2
FEATURE [Sketcher::SketchObject] Sketch1689
  MapMode = 5
  Placement = pos=(0,0,20) rot=(0,0,1;0rad)
  Support = -> [Fillet206]
  sketch-geometry (4):
    g0: LineSegment StartX=0 StartY=0 StartZ=0 EndX=56.5 EndY=0 EndZ=0
    g1: LineSegment StartX=56.5 StartY=0 StartZ=0 EndX=56.5 EndY=25 EndZ=0
    g2: LineSegment StartX=56.5 StartY=25 StartZ=0 EndX=0 EndY=25 EndZ=0
    g3: LineSegment StartX=0 StartY=25 StartZ=0 EndX=0 EndY=0 EndZ=0
  constraints (11):
    c: Coincident(g0,g1)
    c: Coincident(g1,g2)
    c: Coincident(g2,g3)
    c: Coincident(g3,g0)
    c: Horizontal(g0)
    c: Horizontal(g2)
    c: Vertical(g1)
    c: Vertical(g3)
    c: Coincident(g0,g-1)
    c: DistanceY(g3,g3) = 25
    c: DistanceX(g2,g2) = 56.5
FEATURE [PartDesign::Pocket] Pocket596  label="Counterpart Pocket003"
  BaseFeature = -> Fillet206
  Length = 10
  Length2 = 100
  Profile = -> Sketch1689
  Type = 0
FEATURE [PartDesign::Pad] Pad709  label="Extend Baseplate003"
  BaseFeature = -> Pocket596
  Length = 12
  Length2 = 100
  Profile = -> Pocket596 [Face40]
  Type = 0
FEATURE [Sketcher::SketchObject] Sketch1603
  MapMode = 5
  Placement = pos=(0,0,32) rot=(0,0,1;0rad)
  Support = -> [Pad709]
  sketch-geometry (4):
    g0: LineSegment StartX=48.5 StartY=25 StartZ=0 EndX=56.5 EndY=25 EndZ=0
    g1: LineSegment StartX=56.5 StartY=25 StartZ=0 EndX=56.5 EndY=30 EndZ=0
    g2: LineSegment StartX=56.5 StartY=30 StartZ=0 EndX=48.5 EndY=30 EndZ=0
    g3: LineSegment StartX=48.5 StartY=30 StartZ=0 EndX=48.5 EndY=25 EndZ=0
  constraints (12):
    c: Coincident(g0,g1)
    c: Coincident(g1,g2)
    c: Coincident(g2,g3)
    c: Coincident(g3,g0)
    c: Horizontal(g0)
    c: Horizontal(g2)
    c: Vertical(g1)
    c: Vertical(g3)
    c: DistanceY(g3,g3) = 5
    c: DistanceY(g-1,g0) = 25
    c: DistanceX(g2,g2) = 8
    c: DistanceX(g-1,g2) = 48.5
FEATURE [PartDesign::Pocket] Pocket599  label="Remove Extension Servocover003"
  BaseFeature = -> Pad709
  Length = 13
  Length2 = 100
  Profile = -> Sketch1603
  Type = 0
FEATURE [Sketcher::SketchObject] Sketch1593
  MapMode = 5
  Placement = pos=(0,30,0) rot=(0,0.707107,0.707107;3.14159rad)
  Support = -> [Pocket599]
  sketch-geometry (7):
    g0: ArcOfCircle CenterX=22.5 CenterY=65.1875 CenterZ=0 NormalX=0 NormalY=0 NormalZ=1 AngleXU=0 Radius=45.1875 StartAngle=4.19118 EndAngle=4.71239
    g1: LineSegment StartX=-56.5 StartY=33 StartZ=0 EndX=95 EndY=33 EndZ=0
    g2: LineSegment StartX=95 StartY=33 StartZ=0 EndX=95 EndY=20 EndZ=0
    g3: LineSegment StartX=95 StartY=20 StartZ=0 EndX=22.5 EndY=20 EndZ=0
    g4: ArcOfCircle CenterX=-22.5 CenterY=-13.1875 CenterZ=0 NormalX=0 NormalY=0 NormalZ=1 AngleXU=0 Radius=45.1875 StartAngle=1.04959 EndAngle=1.5708
    g5: LineSegment StartX=-22.5 StartY=32 StartZ=0 EndX=-56.5 EndY=32 EndZ=0
    g6: LineSegment StartX=-56.5 StartY=32 StartZ=0 EndX=-56.5 EndY=33 EndZ=0
  constraints (21):
    c: Horizontal(g1)
    c: Coincident(g2,g1)
    c: Vertical(g2)
    c: Coincident(g3,g2)
    c: Horizontal(g3)
    c: Tangent(g3,g0) = 1.5708
    c: DistanceX(g0,g0) = 22.5
    c: DistanceY(g0,g1) = 7
    c: DistanceY(g2,g2) = 13
    c: PointOnObject(g0,g-2)
    c: DistanceY(g-1,g2) = 20
    c: Tangent(g4,g0) = 1.5708
    c: Horizontal(g5)
    c: Coincident(g6,g5)
    c: Coincident(g1,g6)
    c: Vertical(g6)
    c: Tangent(g5,g4) = -1.5708
    c: DistanceY(g6,g6) = 1
    c: DistanceX(g5,g0) = 56.5
    c: DistanceX(g0,g1) = 95
    c: DistanceX(g4,g0) = 22.5
FEATURE [PartDesign::Pocket] Pocket593  label="Swing Leg003"
  BaseFeature = -> Pocket599
  Length = 35
  Length2 = 100
  Profile = -> Sketch1593
  Type = 0
FEATURE [PartDesign::Pad] Pad715  label="Baseblock015"
  Length = 26.6
  Length2 = 100
  Profile = -> Sketch1597
  Type = 0
FEATURE [Sketcher::SketchObject] Sketch1547
  MapMode = 5
  Placement = pos=(0,0,26.6) rot=(0,0,1;0rad)
  Support = -> [Pad715]
  sketch-geometry (4):
    g0: LineSegment StartX=-10 StartY=-26.8 StartZ=0 EndX=10 EndY=-26.8 EndZ=0
    g1: LineSegment StartX=10 StartY=-26.8 StartZ=0 EndX=10 EndY=26.8 EndZ=0
    g2: LineSegment StartX=10 StartY=26.8 StartZ=0 EndX=-10 EndY=26.8 EndZ=0
    g3: LineSegment StartX=-10 StartY=26.8 StartZ=0 EndX=-10 EndY=-26.8 EndZ=0
  constraints (10):
    c: Coincident(g0,g1)
    c: Coincident(g1,g2)
    c: Coincident(g2,g3)
    c: Coincident(g3,g0)
    c: Horizontal(g0)
    c: Vertical(g3)
    c: Symmetric(g1,g2,g-2)
    c: Symmetric(g1,g0,g-1)
    c: DistanceX(g2,g2) = 20
    c: DistanceY(g1,g1) = 53.6
FEATURE [PartDesign::Pad] Pad717  label="M3x8 Thread088"
  BaseFeature = -> Pad710
  Length = 8
  Length2 = 100
  Profile = -> Sketch1608
  Type = 0
FEATURE [Sketcher::SketchObject] Sketch1611
  MapMode = 5
  Placement = pos=(0,0,0) rot=(1,0,0;3.14159rad)
  Support = -> [Pad717]
  sketch-geometry (7):
    g0: LineSegment StartX=1.275 StartY=0.736122 StartZ=0 EndX=0 EndY=1.47224 EndZ=0
    g1: LineSegment StartX=0 StartY=1.47224 StartZ=0 EndX=-1.275 EndY=0.736122 EndZ=0
    g2: LineSegment StartX=-1.275 StartY=0.736122 StartZ=0 EndX=-1.275 EndY=-0.736122 EndZ=0
    g3: LineSegment StartX=-1.275 StartY=-0.736122 StartZ=0 EndX=1.34766e-11 EndY=-1.47224 EndZ=0
    g4: LineSegment StartX=1.34766e-11 StartY=-1.47224 StartZ=0 EndX=1.275 EndY=-0.736122 EndZ=0
    g5: LineSegment StartX=1.275 StartY=-0.736122 StartZ=0 EndX=1.275 EndY=0.736122 EndZ=0
    g6: Circle [constr] CenterX=0 CenterY=0 CenterZ=0 NormalX=0 NormalY=0 NormalZ=1 AngleXU=0 Radius=1.47224
  constraints (16):
    c: Coincident(g0,g1)
    c: Coincident(g1,g2)
    c: Coincident(g2,g3)
    c: Coincident(g3,g4)
    c: Coincident(g4,g5)
    c: Coincident(g5,g0)
    c: Equal(g0, g1-g5) x5
    c: PointOnObject(g0,g6)
    c: PointOnObject(g1,g6)
    c: PointOnObject(g2,g6)
    c: PointOnObject(g3,g6)
    c: PointOnObject(g4,g6)
    c: PointOnObject(g5,g6)
    c: Coincident(g6,g-1)
    c: PointOnObject(g0,g-2)
    c: DistanceX(g1,g0) = 2.55
FEATURE [PartDesign::Pocket] Pocket619  label="M3x8 Wrench092"
  BaseFeature = -> Pad717
  Length = 1.3
  Length2 = 100
  Profile = -> Sketch1611
  Type = 0
FEATURE [PartDesign::Groove] Groove149  label="M3 Nut Smooth141"
  Angle = 360
  Axis = (-2e-16,3e-16,1)
  Base = (0,0,0)
  BaseFeature = -> Pad706
  Profile = -> Sketch1594
  ReferenceAxis = -> Sketch1594 [V_Axis]
  Reversed = true
FEATURE [PartDesign::Chamfer] Chamfer328  label="M3 Nut Smooth Hole138"
  Base = -> Groove149 [Edge24,Edge23]
  BaseFeature = -> Groove149
  Size = 0.2
FEATURE [PartDesign::Pad] Pad722  label="M3x20 Thread064"
  BaseFeature = -> Pad713
  Length = 20
  Length2 = 100
  Profile = -> Sketch1582
  Type = 0
FEATURE [Sketcher::SketchObject] Sketch1586
  MapMode = 5
  Placement = pos=(0,0,0) rot=(1,0,0;3.14159rad)
  Support = -> [Pad722]
  sketch-geometry (7):
    g0: LineSegment StartX=1.275 StartY=0.736122 StartZ=0 EndX=0 EndY=1.47224 EndZ=0
    g1: LineSegment StartX=0 StartY=1.47224 StartZ=0 EndX=-1.275 EndY=0.736122 EndZ=0
    g2: LineSegment StartX=-1.275 StartY=0.736122 StartZ=0 EndX=-1.275 EndY=-0.736122 EndZ=0
    g3: LineSegment StartX=-1.275 StartY=-0.736122 StartZ=0 EndX=1.34766e-11 EndY=-1.47224 EndZ=0
    g4: LineSegment StartX=1.34766e-11 StartY=-1.47224 StartZ=0 EndX=1.275 EndY=-0.736122 EndZ=0
    g5: LineSegment StartX=1.275 StartY=-0.736122 StartZ=0 EndX=1.275 EndY=0.736122 EndZ=0
    g6: Circle [constr] CenterX=0 CenterY=0 CenterZ=0 NormalX=0 NormalY=0 NormalZ=1 AngleXU=0 Radius=1.47224
  constraints (16):
    c: Coincident(g0,g1)
    c: Coincident(g1,g2)
    c: Coincident(g2,g3)
    c: Coincident(g3,g4)
    c: Coincident(g4,g5)
    c: Coincident(g5,g0)
    c: Equal(g0, g1-g5) x5
    c: PointOnObject(g0,g6)
    c: PointOnObject(g1,g6)
    c: PointOnObject(g2,g6)
    c: PointOnObject(g3,g6)
    c: PointOnObject(g4,g6)
    c: PointOnObject(g5,g6)
    c: Coincident(g6,g-1)
    c: PointOnObject(g0,g-2)
    c: DistanceX(g1,g0) = 2.55
FEATURE [PartDesign::Pocket] Pocket622  label="M3x20 Wrench064"
  BaseFeature = -> Pad722
  Length = 1.3
  Length2 = 100
  Profile = -> Sketch1586
  Type = 0
FEATURE [PartDesign::Chamfer] Chamfer313  label="M3x20 Smooth059"
  Base = -> Pocket622 [Face11,Edge2,Edge24,Edge3]
  BaseFeature = -> Pocket622
  Size = 0.2
FEATURE [PartDesign::Revolution] Revolution039
  Angle = 360
  Axis = (0,2e-16,1)
  Base = (0,0,0)
  Placement = pos=(0,0,0) rot=(1,0,0;1.5708rad)
  Profile = -> Sketch1762
  ReferenceAxis = -> Sketch1762 [V_Axis]
FEATURE [PartDesign::Fillet] Fillet225
  Base = -> Revolution039 [Face2,Face6,Edge1,Edge11,Face4]
  BaseFeature = -> Revolution039
  Placement = pos=(0,0,0) rot=(1,0,0;1.5708rad)
  Radius = 0.25
FEATURE [PartDesign::Pad] Pad728  label="M3x20 Head065"
  Length = 3
  Length2 = 100
  Profile = -> Sketch1574
  Type = 0
FEATURE [Sketcher::SketchObject] Sketch1551
  MapMode = 5
  Placement = pos=(0,0,3) rot=(0,0,1;0rad)
  Support = -> [Pad728]
  sketch-geometry (1):
    g0: Circle CenterX=0 CenterY=0 CenterZ=0 NormalX=0 NormalY=0 NormalZ=1 AngleXU=0 Radius=1.5
  constraints (2):
    c: Coincident(g0,g-1)
    c: Radius(g0) = 1.5
FEATURE [PartDesign::Pad] Pad701  label="M3x20 Thread063"
  BaseFeature = -> Pad728
  Length = 20
  Length2 = 100
  Profile = -> Sketch1551
  Type = 0
FEATURE [Sketcher::SketchObject] Sketch1573
  MapMode = 5
  Placement = pos=(0,0,0) rot=(1,0,0;3.14159rad)
  Support = -> [Pad701]
  sketch-geometry (7):
    g0: LineSegment StartX=1.275 StartY=0.736122 StartZ=0 EndX=0 EndY=1.47224 EndZ=0
    g1: LineSegment StartX=0 StartY=1.47224 StartZ=0 EndX=-1.275 EndY=0.736122 EndZ=0
    g2: LineSegment StartX=-1.275 StartY=0.736122 StartZ=0 EndX=-1.275 EndY=-0.736122 EndZ=0
    g3: LineSegment StartX=-1.275 StartY=-0.736122 StartZ=0 EndX=1.34766e-11 EndY=-1.47224 EndZ=0
    g4: LineSegment StartX=1.34766e-11 StartY=-1.47224 StartZ=0 EndX=1.275 EndY=-0.736122 EndZ=0
    g5: LineSegment StartX=1.275 StartY=-0.736122 StartZ=0 EndX=1.275 EndY=0.736122 EndZ=0
    g6: Circle [constr] CenterX=0 CenterY=0 CenterZ=0 NormalX=0 NormalY=0 NormalZ=1 AngleXU=0 Radius=1.47224
  constraints (16):
    c: Coincident(g0,g1)
    c: Coincident(g1,g2)
    c: Coincident(g2,g3)
    c: Coincident(g3,g4)
    c: Coincident(g4,g5)
    c: Coincident(g5,g0)
    c: Equal(g0, g1-g5) x5
    c: PointOnObject(g0,g6)
    c: PointOnObject(g1,g6)
    c: PointOnObject(g2,g6)
    c: PointOnObject(g3,g6)
    c: PointOnObject(g4,g6)
    c: PointOnObject(g5,g6)
    c: Coincident(g6,g-1)
    c: PointOnObject(g0,g-2)
    c: DistanceX(g1,g0) = 2.55
FEATURE [PartDesign::Pocket] Pocket621  label="M3x20 Wrench063"
  BaseFeature = -> Pad701
  Length = 1.3
  Length2 = 100
  Profile = -> Sketch1573
  Type = 0
FEATURE [PartDesign::Chamfer] Chamfer312  label="M3x20 Smooth058"
  Base = -> Pocket621 [Face11,Edge2,Edge24,Edge3]
  BaseFeature = -> Pocket621
  Size = 0.2
FEATURE [PartDesign::Pad] Pad729  label="M3 Nut Primitive142"
  Length = 1.2
  Length2 = 1.2
  Profile = -> Sketch1566
  Type = 4
FEATURE [Sketcher::SketchObject] Sketch1604
  ExternalGeometry = -> [Pad729]
  MapMode = 5
  Placement = pos=(0,0,0) rot=(0.57735,0.57735,0.57735;2.0944rad)
  Support = -> [YZ_Plane585]
  sketch-geometry (6):
    g0: LineSegment StartX=-2.67543 StartY=1.2 StartZ=0 EndX=-3.67543 EndY=1.2 EndZ=0
    g1: LineSegment StartX=-3.67543 StartY=1.2 StartZ=0 EndX=-3.67543 EndY=-1.2 EndZ=0
    g2: LineSegment StartX=-3.67543 StartY=-1.2 StartZ=0 EndX=-2.67543 EndY=-1.2 EndZ=0
    g3: LineSegment StartX=-2.67543 StartY=-1.2 StartZ=0 EndX=-3.17543 EndY=-1 EndZ=0
    g4: LineSegment StartX=-3.17543 StartY=-1 StartZ=0 EndX=-3.17543 EndY=1 EndZ=0
    g5: LineSegment StartX=-3.17543 StartY=1 StartZ=0 EndX=-2.67543 EndY=1.2 EndZ=0
  constraints (15):
    c: Horizontal(g0)
    c: Coincident(g0,g1)
    c: Coincident(g1,g2)
    c: Coincident(g2,g3)
    c: Coincident(g3,g4)
    c: Coincident(g4,g5)
    c: Coincident(g5,g0)
    c: Symmetric(g4,g3,g-1)
    c: Symmetric(g0,g2,g-1)
    c: Symmetric(g1,g0,g-1)
    c: DistanceX(g0,g4) = 0.5
    c: DistanceY(g3,g4) = 2
    c: DistanceY(g1,g0) = 2.4
    c: PointOnObject(g3,g-3)
    c: DistanceX(g4,g0) = 0.5
FEATURE [PartDesign::Groove] Groove146  label="M3 Nut Smooth138"
  Angle = 360
  Axis = (-2e-16,3e-16,1)
  Base = (0,0,0)
  BaseFeature = -> Pad729
  Profile = -> Sketch1604
  ReferenceAxis = -> Sketch1604 [V_Axis]
  Reversed = true
FEATURE [PartDesign::Chamfer] Chamfer309  label="M3 Nut Smooth Hole130"
  Base = -> Groove146 [Edge24,Edge23]
  BaseFeature = -> Groove146
  Size = 0.2
FEATURE [PartDesign::Pad] Pad731  label="M3x20 Thread066"
  BaseFeature = -> Pad700
  Length = 20
  Length2 = 100
  Profile = -> Sketch1578
  Type = 0
FEATURE [Sketcher::SketchObject] Sketch1674
  MapMode = 5
  Placement = pos=(0,0,0) rot=(1,0,0;3.14159rad)
  Support = -> [Pad731]
  sketch-geometry (7):
    g0: LineSegment StartX=1.275 StartY=0.736122 StartZ=0 EndX=0 EndY=1.47224 EndZ=0
    g1: LineSegment StartX=0 StartY=1.47224 StartZ=0 EndX=-1.275 EndY=0.736122 EndZ=0
    g2: LineSegment StartX=-1.275 StartY=0.736122 StartZ=0 EndX=-1.275 EndY=-0.736122 EndZ=0
    g3: LineSegment StartX=-1.275 StartY=-0.736122 StartZ=0 EndX=1.34766e-11 EndY=-1.47224 EndZ=0
    g4: LineSegment StartX=1.34766e-11 StartY=-1.47224 StartZ=0 EndX=1.275 EndY=-0.736122 EndZ=0
    g5: LineSegment StartX=1.275 StartY=-0.736122 StartZ=0 EndX=1.275 EndY=0.736122 EndZ=0
    g6: Circle [constr] CenterX=0 CenterY=0 CenterZ=0 NormalX=0 NormalY=0 NormalZ=1 AngleXU=0 Radius=1.47224
  constraints (16):
    c: Coincident(g0,g1)
    c: Coincident(g1,g2)
    c: Coincident(g2,g3)
    c: Coincident(g3,g4)
    c: Coincident(g4,g5)
    c: Coincident(g5,g0)
    c: Equal(g0, g1-g5) x5
    c: PointOnObject(g0,g6)
    c: PointOnObject(g1,g6)
    c: PointOnObject(g2,g6)
    c: PointOnObject(g3,g6)
    c: PointOnObject(g4,g6)
    c: PointOnObject(g5,g6)
    c: Coincident(g6,g-1)
    c: PointOnObject(g0,g-2)
    c: DistanceX(g1,g0) = 2.55
FEATURE [PartDesign::Pocket] Pocket623  label="M3x20 Wrench065"
  BaseFeature = -> Pad731
  Length = 1.3
  Length2 = 100
  Profile = -> Sketch1674
  Type = 0
FEATURE [PartDesign::Chamfer] Chamfer307  label="M3x20 Smooth057"
  Base = -> Pocket623 [Face11,Edge2,Edge24,Edge3]
  BaseFeature = -> Pocket623
  Size = 0.2
FEATURE [PartDesign::Pad] Pad736
  Length = 10
  Length2 = 100
  Placement = pos=(0,0,0) rot=(1,0,0;1.5708rad)
  Profile = -> Sketch1651
  Reversed = true
  Type = 0
FEATURE [PartDesign::Pad] Pad737
  Length = 5
  Length2 = 100
  Profile = -> Sketch1644
  Type = 0
FEATURE [Sketcher::SketchObject] Sketch1645
  ExternalGeometry = -> [Pad737]
  MapMode = 5
  Placement = pos=(0,0,5) rot=(0,0,1;0rad)
  Support = -> [Pad737]
  sketch-geometry (1):
    g0: Circle CenterX=0 CenterY=10.15 CenterZ=0 NormalX=0 NormalY=0 NormalZ=1 AngleXU=0 Radius=1.5
  constraints (2):
    c: Coincident(g0,g-3)
    c: Radius(g0) = 1.5
FEATURE [PartDesign::Pocket] Pocket572
  BaseFeature = -> Pad737
  Length = 4
  Length2 = 100
  Profile = -> Sketch1645
  Type = 0
FEATURE [PartDesign::Chamfer] Chamfer336
  Base = -> Pocket572 [Edge3]
  BaseFeature = -> Pocket572
  Size = 0.25
FEATURE [PartDesign::Pad] Pad742  label="M3x20 Head069"
  Length = 3
  Length2 = 100
  Profile = -> Sketch1652
  Type = 0
FEATURE [Sketcher::SketchObject] Sketch1657
  MapMode = 5
  Placement = pos=(0,0,3) rot=(0,0,1;0rad)
  Support = -> [Pad742]
  sketch-geometry (1):
    g0: Circle CenterX=0 CenterY=0 CenterZ=0 NormalX=0 NormalY=0 NormalZ=1 AngleXU=0 Radius=1.5
  constraints (2):
    c: Coincident(g0,g-1)
    c: Radius(g0) = 1.5
FEATURE [PartDesign::Pad] Pad663  label="M3x20 Thread058"
  BaseFeature = -> Pad742
  Length = 20
  Length2 = 100
  Profile = -> Sketch1657
  Type = 0
FEATURE [PartDesign::Revolution] Revolution043
  Angle = 360
  Axis = (0,2e-16,1)
  Base = (0,0,0)
  Placement = pos=(0,0,0) rot=(1,0,0;1.5708rad)
  Profile = -> Sketch1761
  ReferenceAxis = -> Sketch1761 [V_Axis]
FEATURE [PartDesign::Revolution] Revolution044
  Angle = 360
  Axis = (0,2e-16,1)
  Base = (0,0,0)
  Placement = pos=(0,0,0) rot=(1,0,0;1.5708rad)
  Profile = -> Sketch1766
  ReferenceAxis = -> Sketch1766 [V_Axis]
FEATURE [PartDesign::Fillet] Fillet229
  Base = -> Revolution044 [Face2,Face6,Edge1,Edge11,Face4]
  BaseFeature = -> Revolution044
  Placement = pos=(0,0,0) rot=(1,0,0;1.5708rad)
  Radius = 0.25
FEATURE [PartDesign::Pad] Pad749  label="M3x20 Head070"
  Length = 3
  Length2 = 100
  Profile = -> Sketch1638
  Type = 0
FEATURE [PartDesign::Pad] Pad751
  Length = 10
  Length2 = 100
  Placement = pos=(0,0,0) rot=(1,0,0;1.5708rad)
  Profile = -> Sketch1646
  Reversed = true
  Type = 0
FEATURE [PartDesign::Pad] Pad753  label="M3x20 Head071"
  Length = 3
  Length2 = 100
  Profile = -> Sketch1650
  Type = 0
FEATURE [PartDesign::Pad] Pad756  label="M3x20 Thread070"
  BaseFeature = -> Pad653
  Length = 20
  Length2 = 100
  Profile = -> Sketch1658
  Type = 0
FEATURE [Sketcher::SketchObject] Sketch1643
  MapMode = 5
  Placement = pos=(0,0,0) rot=(1,0,0;3.14159rad)
  Support = -> [Pad756]
  sketch-geometry (7):
    g0: LineSegment StartX=1.275 StartY=0.736122 StartZ=0 EndX=0 EndY=1.47224 EndZ=0
    g1: LineSegment StartX=0 StartY=1.47224 StartZ=0 EndX=-1.275 EndY=0.736122 EndZ=0
    g2: LineSegment StartX=-1.275 StartY=0.736122 StartZ=0 EndX=-1.275 EndY=-0.736122 EndZ=0
    g3: LineSegment StartX=-1.275 StartY=-0.736122 StartZ=0 EndX=1.34766e-11 EndY=-1.47224 EndZ=0
    g4: LineSegment StartX=1.34766e-11 StartY=-1.47224 StartZ=0 EndX=1.275 EndY=-0.736122 EndZ=0
    g5: LineSegment StartX=1.275 StartY=-0.736122 StartZ=0 EndX=1.275 EndY=0.736122 EndZ=0
    g6: Circle [constr] CenterX=0 CenterY=0 CenterZ=0 NormalX=0 NormalY=0 NormalZ=1 AngleXU=0 Radius=1.47224
  constraints (16):
    c: Coincident(g0,g1)
    c: Coincident(g1,g2)
    c: Coincident(g2,g3)
    c: Coincident(g3,g4)
    c: Coincident(g4,g5)
    c: Coincident(g5,g0)
    c: Equal(g0, g1-g5) x5
    c: PointOnObject(g0,g6)
    c: PointOnObject(g1,g6)
    c: PointOnObject(g2,g6)
    c: PointOnObject(g3,g6)
    c: PointOnObject(g4,g6)
    c: PointOnObject(g5,g6)
    c: Coincident(g6,g-1)
    c: PointOnObject(g0,g-2)
    c: DistanceX(g1,g0) = 2.55
FEATURE [PartDesign::Pocket] Pocket573  label="M3x20 Wrench060"
  BaseFeature = -> Pad756
  Length = 1.3
  Length2 = 100
  Profile = -> Sketch1643
  Type = 0
FEATURE [PartDesign::Chamfer] Chamfer351  label="M3x20 Smooth065"
  Base = -> Pocket573 [Face11,Edge2,Edge24,Edge3]
  BaseFeature = -> Pocket573
  Size = 0.2
FEATURE [PartDesign::Revolution] Revolution047
  Angle = 360
  Axis = (0,2e-16,1)
  Base = (0,0,0)
  Placement = pos=(0,0,0) rot=(1,0,0;1.5708rad)
  Profile = -> Sketch1718
  ReferenceAxis = -> Sketch1718 [V_Axis]
FEATURE [PartDesign::Fillet] Fillet222
  Base = -> Revolution047 [Face2,Face6,Edge1,Edge11,Face4]
  BaseFeature = -> Revolution047
  Placement = pos=(0,0,0) rot=(1,0,0;1.5708rad)
  Radius = 0.25
FEATURE [PartDesign::Fillet] Fillet232
  Base = -> Revolution043 [Face2,Face6,Edge1,Edge11,Face4]
  BaseFeature = -> Revolution043
  Placement = pos=(0,0,0) rot=(1,0,0;1.5708rad)
  Radius = 0.25
FEATURE [PartDesign::Fillet] Fillet233  label="Servocable 003"
  Base = -> Pocket593 [Edge144,Edge135]
  BaseFeature = -> Pocket593
  Radius = 3
FEATURE [Sketcher::SketchObject] Sketch1584
  ExternalGeometry = -> [Fillet233]
  MapMode = 5
  Placement = pos=(0,4.4e-15,20) rot=(0,0,1;0rad)
  Support = -> [Fillet233]
  sketch-geometry (12):
    g0: Circle CenterX=-25.3678 CenterY=16.4091 CenterZ=0 NormalX=0 NormalY=0 NormalZ=1 AngleXU=0 Radius=1.6
    g1: LineSegment [constr] StartX=-23 StartY=18.7769 StartZ=0 EndX=-26.2345 EndY=19.6436 EndZ=0
    g2: LineSegment [constr] StartX=-26.2345 StartY=19.6436 StartZ=0 EndX=-28.6024 EndY=17.2757 EndZ=0
    g3: LineSegment [constr] StartX=-28.6024 StartY=17.2757 StartZ=0 EndX=-27.7357 EndY=14.0412 EndZ=0
    g4: LineSegment [constr] StartX=-27.7357 StartY=14.0412 StartZ=0 EndX=-24.5012 EndY=13.1745 EndZ=0
    g5: LineSegment [constr] StartX=-24.5012 StartY=13.1745 StartZ=0 EndX=-22.1333 EndY=15.5424 EndZ=0
    g6: LineSegment [constr] StartX=-22.1333 StartY=15.5424 StartZ=0 EndX=-23 EndY=18.7769 EndZ=0
    g7: Circle [constr] CenterX=-25.3678 CenterY=16.4091 CenterZ=0 NormalX=0 NormalY=0 NormalZ=1 AngleXU=0 Radius=3.34863
    g8: Circle CenterX=4 CenterY=20 CenterZ=0 NormalX=0 NormalY=0 NormalZ=1 AngleXU=0 Radius=1.6
    g9: Circle CenterX=52.5 CenterY=20 CenterZ=0 NormalX=0 NormalY=0 NormalZ=1 AngleXU=0 Radius=1.6
    g10: Circle CenterX=52.5 CenterY=10 CenterZ=0 NormalX=0 NormalY=0 NormalZ=1 AngleXU=0 Radius=1.6
    g11: Circle CenterX=4 CenterY=10 CenterZ=0 NormalX=0 NormalY=0 NormalZ=1 AngleXU=0 Radius=1.6
  constraints (30):
    c: Radius(g0) = 1.6
    c: Coincident(g1,g2)
    c: Coincident(g2,g3)
    c: Coincident(g3,g4)
    c: Coincident(g4,g5)
    c: Coincident(g5,g6)
    c: Coincident(g6,g1)
    c: Equal(g1, g2-g6) x5
    c: PointOnObject(g1,g7)
    c: PointOnObject(g2,g7)
    c: PointOnObject(g3,g7)
    c: PointOnObject(g4,g7)
    c: PointOnObject(g5,g7)
    c: PointOnObject(g6,g7)
    c: Coincident(g7,g0)
    c: Distance(g4,g2) = 5.8
    c: Coincident(g1,g-3)
    c: Angle(g5) = 0.785398
    c: Horizontal(g8,g9)
    c: Horizontal(g11,g10)
    c: Vertical(g10,g9)
    c: Vertical(g8,g11)
    c: Equal(g11,g8)
    c: Equal(g8,g9)
    c: Equal(g9,g10)
    c: Equal(g8,g0)
    c: DistanceX(g11,g10) = 48.5
    c: DistanceY(g11,g8) = 10
    c: DistanceY(g-1,g11) = 10
    c: DistanceX(g-1,g11) = 4
FEATURE [PartDesign::Pocket] Pocket591  label="Screwhole003"
  BaseFeature = -> Fillet233
  Length = 20
  Length2 = 100
  Profile = -> Sketch1584
  Type = 0
FEATURE [Sketcher::SketchObject] Sketch1606
  MapMode = 5
  Placement = pos=(0,4.4e-15,20) rot=(0,0,1;0rad)
  Support = -> [Pocket591]
  sketch-geometry (5):
    g0: ArcOfCircle CenterX=-80 CenterY=15 CenterZ=0 NormalX=0 NormalY=0 NormalZ=1 AngleXU=0 Radius=12.5 StartAngle=2.35619 EndAngle=5.49779
    g1: LineSegment [constr] StartX=-88.8388 StartY=23.8388 StartZ=0 EndX=-71.1612 EndY=6.16117 EndZ=0
    g2: LineSegment StartX=-88.8388 StartY=23.8388 StartZ=0 EndX=-92.3744 EndY=27.3744 EndZ=0
    g3: LineSegment StartX=-71.1612 StartY=6.16117 StartZ=0 EndX=-67.6256 EndY=2.62563 EndZ=0
    g4: ArcOfCircle CenterX=-80 CenterY=15 CenterZ=0 NormalX=0 NormalY=0 NormalZ=1 AngleXU=0 Radius=17.5 StartAngle=2.35619 EndAngle=5.49779
  constraints (15):
    c: Radius(g0) = 12.5
    c: DistanceX(g0,g-1) = 80
    c: DistanceY(g-1,g0) = 15
    c: Coincident(g1,g0)
    c: Coincident(g1,g0)
    c: Angle(g1) = -0.785398
    c: PointOnObject(g0,g1)
    c: Coincident(g2,g0)
    c: Coincident(g3,g0)
    c: Coincident(g4,g0)
    c: Coincident(g4,g2)
    c: Coincident(g4,g3)
    c: Tangent(g2,g1)
    c: Tangent(g1,g3)
    c: Radius(g4) = 17.5
FEATURE [PartDesign::Pocket] Pocket597  label="Rubberfoot Pocket003"
  BaseFeature = -> Pocket591
  Length = 20
  Length2 = 100
  Profile = -> Sketch1606
  Type = 0
FEATURE [Sketcher::SketchObject] Sketch1592
  AttachmentOffset = pos=(0,0,-3) rot=(0,0,1;0rad)
  ExternalGeometry = -> [Pocket597]
  MapMode = 5
  Placement = pos=(0,3.7e-15,17) rot=(0,0,1;0rad)
  Support = -> [Pocket597]
  sketch-geometry (10):
    g0: LineSegment [constr] StartX=-52.5747 StartY=33.6444 StartZ=0 EndX=-49.7647 EndY=34.4507 EndZ=0
    g1: LineSegment StartX=-49.7647 StartY=34.4507 StartZ=0 EndX=-52.5747 EndY=33.6444 EndZ=0
    g2: LineSegment StartX=-52.5747 StartY=33.6444 StartZ=0 EndX=-55.0934 EndY=32.1605 EndZ=0
    g3: LineSegment StartX=-55.0934 StartY=32.1605 StartZ=0 EndX=-57.1605 EndY=30.0934 EndZ=0
    g4: LineSegment StartX=-57.1605 StartY=30.0934 StartZ=0 EndX=-55.0934 EndY=32.1605 EndZ=0
    g5: LineSegment [constr] StartX=-55.0934 StartY=32.1605 StartZ=0 EndX=-52.5747 EndY=33.6444 EndZ=0
    g6: Circle [constr] CenterX=-48 CenterY=23 CenterZ=0 NormalX=0 NormalY=0 NormalZ=1 AngleXU=0 Radius=11.5858
    g7: LineSegment StartX=-55.0934 StartY=32.1605 StartZ=0 EndX=-53.6792 EndY=33.5747 EndZ=0
    g8: LineSegment StartX=-53.6792 StartY=33.5747 StartZ=0 EndX=-53.4871 EndY=33.3827 EndZ=0
    g9: LineSegment StartX=-53.4871 StartY=33.3827 StartZ=0 EndX=-49.7647 EndY=34.4507 EndZ=0
  constraints (23):
    c: Coincident(g0,g1)
    c: Coincident(g1,g2)
    c: Coincident(g2,g3)
    c: Coincident(g3,g4)
    c: Coincident(g4,g5)
    c: Coincident(g5,g0)
    c: Equal(g0, g1-g5) x5
    c: PointOnObject(g0,g6)
    c: PointOnObject(g1,g6)
    c: PointOnObject(g2,g6)
    c: PointOnObject(g3,g6)
    c: PointOnObject(g4,g6)
    c: PointOnObject(g5,g6)
    c: Coincident(g6,g-3)
    c: Angle(g4) = 0.785398
    c: Distance(g1,g3) = 5.8
    c: Coincident(g8,g7)
    c: Coincident(g9,g8)
    c: Coincident(g9,g0)
    c: Tangent(g7,g4) = -1.5708
    c: Tangent(g9,g1)
    c: Perpendicular(g8,g7)
    c: Distance(g7) = 2
FEATURE [Sketcher::SketchObject] Sketch1598
  AttachmentOffset = pos=(0,0,-17) rot=(0,0,1;0rad)
  ExternalGeometry = -> [Pocket597]
  MapMode = 5
  Placement = pos=(0,7e-16,3) rot=(0,0,1;0rad)
  Support = -> [Pocket597]
  sketch-geometry (10):
    g0: LineSegment [constr] StartX=-52.5746 StartY=33.6443 StartZ=0 EndX=-49.7646 EndY=34.4505 EndZ=0
    g1: LineSegment StartX=-49.7646 StartY=34.4505 StartZ=0 EndX=-52.5746 EndY=33.6443 EndZ=0
    g2: LineSegment StartX=-52.5746 StartY=33.6443 StartZ=0 EndX=-55.0933 EndY=32.1604 EndZ=0
    g3: LineSegment StartX=-55.0933 StartY=32.1604 StartZ=0 EndX=-57.1604 EndY=30.0933 EndZ=0
    g4: LineSegment StartX=-57.1604 StartY=30.0933 StartZ=0 EndX=-55.0933 EndY=32.1604 EndZ=0
    g5: LineSegment [constr] StartX=-55.0933 StartY=32.1604 StartZ=0 EndX=-52.5746 EndY=33.6443 EndZ=0
    g6: Circle [constr] CenterX=-48 CenterY=23 CenterZ=0 NormalX=0 NormalY=0 NormalZ=1 AngleXU=0 Radius=11.5857
    g7: LineSegment StartX=-55.0933 StartY=32.1604 StartZ=0 EndX=-53.6791 EndY=33.5746 EndZ=0
    g8: LineSegment StartX=-53.6791 StartY=33.5746 StartZ=0 EndX=-53.487 EndY=33.3826 EndZ=0
    g9: LineSegment StartX=-53.487 StartY=33.3826 StartZ=0 EndX=-49.7646 EndY=34.4505 EndZ=0
  constraints (23):
    c: Coincident(g0,g1)
    c: Coincident(g1,g2)
    c: Coincident(g2,g3)
    c: Coincident(g3,g4)
    c: Coincident(g4,g5)
    c: Coincident(g5,g0)
    c: Equal(g0, g1-g5) x5
    c: PointOnObject(g0,g6)
    c: PointOnObject(g1,g6)
    c: PointOnObject(g2,g6)
    c: PointOnObject(g3,g6)
    c: PointOnObject(g4,g6)
    c: PointOnObject(g5,g6)
    c: Coincident(g6,g-3)
    c: Angle(g4) = 0.785398
    c: Distance(g1,g3) = 5.8
    c: Coincident(g8,g7)
    c: Coincident(g9,g8)
    c: Coincident(g9,g0)
    c: Tangent(g7,g4) = -1.5708
    c: Tangent(g9,g1)
    c: Perpendicular(g8,g7)
    c: Distance(g7) = 2
FEATURE [PartDesign::Pocket] Pocket594  label="Nuthole #007"
  BaseFeature = -> Pocket597
  Length = 3
  Length2 = 100
  Profile = -> Sketch1592
  Type = 0
FEATURE [PartDesign::Pocket] Pocket610  label="Nuthole #008"
  BaseFeature = -> Pocket594
  Length = 3
  Length2 = 100
  Profile = -> Sketch1598
  Reversed = true
  Type = 0
FEATURE [PartDesign::Chamfer] Chamfer339  label="Smooth Nutholes003"
  Base = -> Pocket610 [Edge206,Edge207,Edge141,Edge209,Edge208,Edge225,Edge222,Edge223,Edge224,Edge221]
  BaseFeature = -> Pocket610
  Size = 0.625
FEATURE [Sketcher::SketchObject] Sketch1579
  MapMode = 5
  Placement = pos=(0,0,10) rot=(0,0,1;0rad)
  Support = -> [Chamfer339]
  sketch-geometry (4):
    g0: LineSegment StartX=0 StartY=0 StartZ=0 EndX=56.5 EndY=0 EndZ=0
    g1: LineSegment StartX=56.5 StartY=0 StartZ=0 EndX=56.5 EndY=5 EndZ=0
    g2: LineSegment StartX=56.5 StartY=5 StartZ=0 EndX=0 EndY=5 EndZ=0
    g3: LineSegment StartX=0 StartY=5 StartZ=0 EndX=0 EndY=0 EndZ=0
  constraints (11):
    c: Coincident(g0,g1)
    c: Coincident(g1,g2)
    c: Coincident(g2,g3)
    c: Coincident(g3,g0)
    c: Horizontal(g0)
    c: Horizontal(g2)
    c: Vertical(g1)
    c: Vertical(g3)
    c: Coincident(g0,g-1)
    c: DistanceY(g1,g1) = 5
    c: DistanceX(g2,g2) = 56.5
FEATURE [PartDesign::Pocket] Pocket608  label="Shorten Baseplate003"
  BaseFeature = -> Chamfer339
  Length = 10
  Length2 = 100
  Profile = -> Sketch1579
  Type = 0
FEATURE [PartDesign::Fillet] Fillet208  label="Smooth Corners003"
  Base = -> Pocket608 [Edge232,Edge234,Edge240,Edge242,Edge193,Edge83,Edge85,Edge86,Edge88,Edge170,Edge236,Edge238,Edge258]
  BaseFeature = -> Pocket608
  Radius = 0.4
FEATURE [PartDesign::Chamfer] Chamfer375  label="M3x8 Smooth096"
  Base = -> Pocket619 [Face11,Edge2,Edge24,Edge3]
  BaseFeature = -> Pocket619
  Size = 0.2
FEATURE [Sketcher::SketchObject] Sketch1785
  MapMode = 5
  Support = -> [XY_Plane677]
  sketch-geometry (1):
    g0: Circle CenterX=0 CenterY=0 CenterZ=0 NormalX=0 NormalY=0 NormalZ=1 AngleXU=0 Radius=2.75
  constraints (2):
    c: Coincident(g0,g-1)
    c: Radius(g0) = 2.75
FEATURE [PartDesign::Pad] Pad684  label="M3x20 Head060"
  Length = 3
  Length2 = 100
  Profile = -> Sketch1785
  Type = 0
FEATURE [Sketcher::SketchObject] Sketch1786
  MapMode = 5
  Support = -> [XY_Plane674]
  sketch-geometry (1):
    g0: Circle CenterX=0 CenterY=0 CenterZ=0 NormalX=0 NormalY=0 NormalZ=1 AngleXU=0 Radius=2.75
  constraints (2):
    c: Coincident(g0,g-1)
    c: Radius(g0) = 2.75
FEATURE [PartDesign::Pad] Pad658  label="M3x20 Head058"
  Length = 3
  Length2 = 100
  Profile = -> Sketch1786
  Type = 0
FEATURE [Sketcher::SketchObject] Sketch1655
  MapMode = 5
  Placement = pos=(0,0,3) rot=(0,0,1;0rad)
  Support = -> [Pad658]
  sketch-geometry (1):
    g0: Circle CenterX=0 CenterY=0 CenterZ=0 NormalX=0 NormalY=0 NormalZ=1 AngleXU=0 Radius=1.5
  constraints (2):
    c: Coincident(g0,g-1)
    c: Radius(g0) = 1.5
FEATURE [PartDesign::Pad] Pad668  label="M3x20 Thread060"
  BaseFeature = -> Pad658
  Length = 20
  Length2 = 100
  Profile = -> Sketch1655
  Type = 0
FEATURE [Sketcher::SketchObject] Sketch1787
  MapMode = 5
  Placement = pos=(0,0,0) rot=(1,0,0;3.14159rad)
  Support = -> [Pad668]
  sketch-geometry (7):
    g0: LineSegment StartX=1.275 StartY=0.736122 StartZ=0 EndX=0 EndY=1.47224 EndZ=0
    g1: LineSegment StartX=0 StartY=1.47224 StartZ=0 EndX=-1.275 EndY=0.736122 EndZ=0
    g2: LineSegment StartX=-1.275 StartY=0.736122 StartZ=0 EndX=-1.275 EndY=-0.736122 EndZ=0
    g3: LineSegment StartX=-1.275 StartY=-0.736122 StartZ=0 EndX=1.34766e-11 EndY=-1.47224 EndZ=0
    g4: LineSegment StartX=1.34766e-11 StartY=-1.47224 StartZ=0 EndX=1.275 EndY=-0.736122 EndZ=0
    g5: LineSegment StartX=1.275 StartY=-0.736122 StartZ=0 EndX=1.275 EndY=0.736122 EndZ=0
    g6: Circle [constr] CenterX=0 CenterY=0 CenterZ=0 NormalX=0 NormalY=0 NormalZ=1 AngleXU=0 Radius=1.47224
  constraints (16):
    c: Coincident(g0,g1)
    c: Coincident(g1,g2)
    c: Coincident(g2,g3)
    c: Coincident(g3,g4)
    c: Coincident(g4,g5)
    c: Coincident(g5,g0)
    c: Equal(g0, g1-g5) x5
    c: PointOnObject(g0,g6)
    c: PointOnObject(g1,g6)
    c: PointOnObject(g2,g6)
    c: PointOnObject(g3,g6)
    c: PointOnObject(g4,g6)
    c: PointOnObject(g5,g6)
    c: Coincident(g6,g-1)
    c: PointOnObject(g0,g-2)
    c: DistanceX(g1,g0) = 2.55
FEATURE [PartDesign::Pocket] Pocket569  label="M3x20 Wrench058"
  BaseFeature = -> Pad668
  Length = 1.3
  Length2 = 100
  Profile = -> Sketch1787
  Type = 0
FEATURE [PartDesign::Chamfer] Chamfer356  label="M3x20 Smooth067"
  Base = -> Pocket569 [Face11,Edge2,Edge24,Edge3]
  BaseFeature = -> Pocket569
  Size = 0.2
FEATURE [Sketcher::SketchObject] Sketch1788
  MapMode = 5
  Placement = pos=(0,0,3) rot=(0,0,1;0rad)
  Support = -> [Pad684]
  sketch-geometry (1):
    g0: Circle CenterX=0 CenterY=0 CenterZ=0 NormalX=0 NormalY=0 NormalZ=1 AngleXU=0 Radius=1.5
  constraints (2):
    c: Coincident(g0,g-1)
    c: Radius(g0) = 1.5
FEATURE [PartDesign::Pad] Pad664  label="M3x20 Thread059"
  BaseFeature = -> Pad684
  Length = 20
  Length2 = 100
  Profile = -> Sketch1788
  Type = 0
FEATURE [Sketcher::SketchObject] Sketch1791
  MapMode = 5
  Placement = pos=(0,0,3) rot=(0,0,1;0rad)
  Support = -> [Pad749]
  sketch-geometry (1):
    g0: Circle CenterX=0 CenterY=0 CenterZ=0 NormalX=0 NormalY=0 NormalZ=1 AngleXU=0 Radius=1.5
  constraints (2):
    c: Coincident(g0,g-1)
    c: Radius(g0) = 1.5
FEATURE [PartDesign::Pad] Pad675  label="M3x20 Thread061"
  BaseFeature = -> Pad749
  Length = 20
  Length2 = 100
  Profile = -> Sketch1791
  Type = 0
FEATURE [Sketcher::SketchObject] Sketch1647
  MapMode = 5
  Placement = pos=(0,0,0) rot=(1,0,0;3.14159rad)
  Support = -> [Pad675]
  sketch-geometry (7):
    g0: LineSegment StartX=1.275 StartY=0.736122 StartZ=0 EndX=0 EndY=1.47224 EndZ=0
    g1: LineSegment StartX=0 StartY=1.47224 StartZ=0 EndX=-1.275 EndY=0.736122 EndZ=0
    g2: LineSegment StartX=-1.275 StartY=0.736122 StartZ=0 EndX=-1.275 EndY=-0.736122 EndZ=0
    g3: LineSegment StartX=-1.275 StartY=-0.736122 StartZ=0 EndX=1.34766e-11 EndY=-1.47224 EndZ=0
    g4: LineSegment StartX=1.34766e-11 StartY=-1.47224 StartZ=0 EndX=1.275 EndY=-0.736122 EndZ=0
    g5: LineSegment StartX=1.275 StartY=-0.736122 StartZ=0 EndX=1.275 EndY=0.736122 EndZ=0
    g6: Circle [constr] CenterX=0 CenterY=0 CenterZ=0 NormalX=0 NormalY=0 NormalZ=1 AngleXU=0 Radius=1.47224
  constraints (16):
    c: Coincident(g0,g1)
    c: Coincident(g1,g2)
    c: Coincident(g2,g3)
    c: Coincident(g3,g4)
    c: Coincident(g4,g5)
    c: Coincident(g5,g0)
    c: Equal(g0, g1-g5) x5
    c: PointOnObject(g0,g6)
    c: PointOnObject(g1,g6)
    c: PointOnObject(g2,g6)
    c: PointOnObject(g3,g6)
    c: PointOnObject(g4,g6)
    c: PointOnObject(g5,g6)
    c: Coincident(g6,g-1)
    c: PointOnObject(g0,g-2)
    c: DistanceX(g1,g0) = 2.55
FEATURE [PartDesign::Pocket] Pocket567  label="M3x20 Wrench057"
  BaseFeature = -> Pad675
  Length = 1.3
  Length2 = 100
  Profile = -> Sketch1647
  Type = 0
FEATURE [PartDesign::Chamfer] Chamfer353  label="M3x20 Smooth066"
  Base = -> Pocket567 [Face11,Edge2,Edge24,Edge3]
  BaseFeature = -> Pocket567
  Size = 0.2
FEATURE [Sketcher::SketchObject] Sketch1792
  MapMode = 5
  Placement = pos=(0,0,3) rot=(0,0,1;0rad)
  Support = -> [Pad753]
  sketch-geometry (1):
    g0: Circle CenterX=0 CenterY=0 CenterZ=0 NormalX=0 NormalY=0 NormalZ=1 AngleXU=0 Radius=1.5
  constraints (2):
    c: Coincident(g0,g-1)
    c: Radius(g0) = 1.5
FEATURE [PartDesign::Pad] Pad750  label="M3x20 Thread069"
  BaseFeature = -> Pad753
  Length = 20
  Length2 = 100
  Profile = -> Sketch1792
  Type = 0
FEATURE [Sketcher::SketchObject] Sketch1796
  MapMode = 5
  Placement = pos=(0,0,0) rot=(1,0,0;3.14159rad)
  Support = -> [Pad664]
  sketch-geometry (7):
    g0: LineSegment StartX=1.275 StartY=0.736122 StartZ=0 EndX=0 EndY=1.47224 EndZ=0
    g1: LineSegment StartX=0 StartY=1.47224 StartZ=0 EndX=-1.275 EndY=0.736122 EndZ=0
    g2: LineSegment StartX=-1.275 StartY=0.736122 StartZ=0 EndX=-1.275 EndY=-0.736122 EndZ=0
    g3: LineSegment StartX=-1.275 StartY=-0.736122 StartZ=0 EndX=1.34766e-11 EndY=-1.47224 EndZ=0
    g4: LineSegment StartX=1.34766e-11 StartY=-1.47224 StartZ=0 EndX=1.275 EndY=-0.736122 EndZ=0
    g5: LineSegment StartX=1.275 StartY=-0.736122 StartZ=0 EndX=1.275 EndY=0.736122 EndZ=0
    g6: Circle [constr] CenterX=0 CenterY=0 CenterZ=0 NormalX=0 NormalY=0 NormalZ=1 AngleXU=0 Radius=1.47224
  constraints (16):
    c: Coincident(g0,g1)
    c: Coincident(g1,g2)
    c: Coincident(g2,g3)
    c: Coincident(g3,g4)
    c: Coincident(g4,g5)
    c: Coincident(g5,g0)
    c: Equal(g0, g1-g5) x5
    c: PointOnObject(g0,g6)
    c: PointOnObject(g1,g6)
    c: PointOnObject(g2,g6)
    c: PointOnObject(g3,g6)
    c: PointOnObject(g4,g6)
    c: PointOnObject(g5,g6)
    c: Coincident(g6,g-1)
    c: PointOnObject(g0,g-2)
    c: DistanceX(g1,g0) = 2.55
FEATURE [PartDesign::Pocket] Pocket635  label="M3x20 Wrench069"
  BaseFeature = -> Pad664
  Length = 1.3
  Length2 = 100
  Profile = -> Sketch1796
  Type = 0
FEATURE [PartDesign::Chamfer] Chamfer345  label="M3x20 Smooth063"
  Base = -> Pocket635 [Face11,Edge2,Edge24,Edge3]
  BaseFeature = -> Pocket635
  Size = 0.2
FEATURE [Sketcher::SketchObject] Sketch1798
  MapMode = 5
  Support = -> [XY_Plane629]
  sketch-geometry (1):
    g0: Circle CenterX=0 CenterY=0 CenterZ=0 NormalX=0 NormalY=0 NormalZ=1 AngleXU=0 Radius=2.75
  constraints (2):
    c: Coincident(g0,g-1)
    c: Radius(g0) = 2.75
FEATURE [PartDesign::Pad] Pad671  label="M3x8 Head082"
  Length = 3
  Length2 = 100
  Profile = -> Sketch1798
  Type = 0
FEATURE [Sketcher::SketchObject] Sketch1790
  MapMode = 5
  Placement = pos=(0,0,3) rot=(0,0,1;0rad)
  Support = -> [Pad671]
  sketch-geometry (1):
    g0: Circle CenterX=0 CenterY=0 CenterZ=0 NormalX=0 NormalY=0 NormalZ=1 AngleXU=0 Radius=1.5
  constraints (2):
    c: Coincident(g0,g-1)
    c: Radius(g0) = 1.5
FEATURE [PartDesign::Pad] Pad660  label="M3x8 Thread080"
  BaseFeature = -> Pad671
  Length = 8
  Length2 = 100
  Profile = -> Sketch1790
  Type = 0
FEATURE [Sketcher::SketchObject] Sketch1783
  MapMode = 5
  Placement = pos=(0,0,0) rot=(1,0,0;3.14159rad)
  Support = -> [Pad660]
  sketch-geometry (7):
    g0: LineSegment StartX=1.275 StartY=0.736122 StartZ=0 EndX=0 EndY=1.47224 EndZ=0
    g1: LineSegment StartX=0 StartY=1.47224 StartZ=0 EndX=-1.275 EndY=0.736122 EndZ=0
    g2: LineSegment StartX=-1.275 StartY=0.736122 StartZ=0 EndX=-1.275 EndY=-0.736122 EndZ=0
    g3: LineSegment StartX=-1.275 StartY=-0.736122 StartZ=0 EndX=1.34766e-11 EndY=-1.47224 EndZ=0
    g4: LineSegment StartX=1.34766e-11 StartY=-1.47224 StartZ=0 EndX=1.275 EndY=-0.736122 EndZ=0
    g5: LineSegment StartX=1.275 StartY=-0.736122 StartZ=0 EndX=1.275 EndY=0.736122 EndZ=0
    g6: Circle [constr] CenterX=0 CenterY=0 CenterZ=0 NormalX=0 NormalY=0 NormalZ=1 AngleXU=0 Radius=1.47224
  constraints (16):
    c: Coincident(g0,g1)
    c: Coincident(g1,g2)
    c: Coincident(g2,g3)
    c: Coincident(g3,g4)
    c: Coincident(g4,g5)
    c: Coincident(g5,g0)
    c: Equal(g0, g1-g5) x5
    c: PointOnObject(g0,g6)
    c: PointOnObject(g1,g6)
    c: PointOnObject(g2,g6)
    c: PointOnObject(g3,g6)
    c: PointOnObject(g4,g6)
    c: PointOnObject(g5,g6)
    c: Coincident(g6,g-1)
    c: PointOnObject(g0,g-2)
    c: DistanceX(g1,g0) = 2.55
FEATURE [PartDesign::Pocket] Pocket568  label="M3x8 Wrench080"
  BaseFeature = -> Pad660
  Length = 1.3
  Length2 = 100
  Profile = -> Sketch1783
  Type = 0
FEATURE [PartDesign::Chamfer] Chamfer367  label="M3x8 Smooth094"
  Base = -> Pocket568 [Face11,Edge2,Edge24,Edge3]
  BaseFeature = -> Pocket568
  Size = 0.2
FEATURE [Sketcher::SketchObject] Sketch1801
  MapMode = 5
  Placement = pos=(0,0,0) rot=(1,0,0;3.14159rad)
  Support = -> [Pad663]
  sketch-geometry (7):
    g0: LineSegment StartX=1.275 StartY=0.736122 StartZ=0 EndX=0 EndY=1.47224 EndZ=0
    g1: LineSegment StartX=0 StartY=1.47224 StartZ=0 EndX=-1.275 EndY=0.736122 EndZ=0
    g2: LineSegment StartX=-1.275 StartY=0.736122 StartZ=0 EndX=-1.275 EndY=-0.736122 EndZ=0
    g3: LineSegment StartX=-1.275 StartY=-0.736122 StartZ=0 EndX=1.34766e-11 EndY=-1.47224 EndZ=0
    g4: LineSegment StartX=1.34766e-11 StartY=-1.47224 StartZ=0 EndX=1.275 EndY=-0.736122 EndZ=0
    g5: LineSegment StartX=1.275 StartY=-0.736122 StartZ=0 EndX=1.275 EndY=0.736122 EndZ=0
    g6: Circle [constr] CenterX=0 CenterY=0 CenterZ=0 NormalX=0 NormalY=0 NormalZ=1 AngleXU=0 Radius=1.47224
  constraints (16):
    c: Coincident(g0,g1)
    c: Coincident(g1,g2)
    c: Coincident(g2,g3)
    c: Coincident(g3,g4)
    c: Coincident(g4,g5)
    c: Coincident(g5,g0)
    c: Equal(g0, g1-g5) x5
    c: PointOnObject(g0,g6)
    c: PointOnObject(g1,g6)
    c: PointOnObject(g2,g6)
    c: PointOnObject(g3,g6)
    c: PointOnObject(g4,g6)
    c: PointOnObject(g5,g6)
    c: Coincident(g6,g-1)
    c: PointOnObject(g0,g-2)
    c: DistanceX(g1,g0) = 2.55
FEATURE [PartDesign::Pocket] Pocket570  label="M3x20 Wrench059"
  BaseFeature = -> Pad663
  Length = 1.3
  Length2 = 100
  Profile = -> Sketch1801
  Type = 0
FEATURE [PartDesign::Chamfer] Chamfer349  label="M3x20 Smooth064"
  Base = -> Pocket570 [Face11,Edge2,Edge24,Edge3]
  BaseFeature = -> Pocket570
  Size = 0.2
FEATURE [Sketcher::SketchObject] Sketch1802
  MapMode = 5
  Support = -> [XY_Plane667]
  sketch-geometry (1):
    g0: Circle CenterX=0 CenterY=0 CenterZ=0 NormalX=0 NormalY=0 NormalZ=1 AngleXU=0 Radius=2.75
  constraints (2):
    c: Coincident(g0,g-1)
    c: Radius(g0) = 2.75
FEATURE [PartDesign::Pad] Pad666  label="M3x20 Head059"
  Length = 3
  Length2 = 100
  Profile = -> Sketch1802
  Type = 0
FEATURE [Sketcher::SketchObject] Sketch1659
  MapMode = 5
  Placement = pos=(0,0,3) rot=(0,0,1;0rad)
  Support = -> [Pad666]
  sketch-geometry (1):
    g0: Circle CenterX=0 CenterY=0 CenterZ=0 NormalX=0 NormalY=0 NormalZ=1 AngleXU=0 Radius=1.5
  constraints (2):
    c: Coincident(g0,g-1)
    c: Radius(g0) = 1.5
FEATURE [PartDesign::Pad] Pad662  label="M3x20 Thread057"
  BaseFeature = -> Pad666
  Length = 20
  Length2 = 100
  Profile = -> Sketch1659
  Type = 0
FEATURE [Sketcher::SketchObject] Sketch1632
  MapMode = 5
  Placement = pos=(0,0,0) rot=(1,0,0;3.14159rad)
  Support = -> [Pad662]
  sketch-geometry (7):
    g0: LineSegment StartX=1.275 StartY=0.736122 StartZ=0 EndX=0 EndY=1.47224 EndZ=0
    g1: LineSegment StartX=0 StartY=1.47224 StartZ=0 EndX=-1.275 EndY=0.736122 EndZ=0
    g2: LineSegment StartX=-1.275 StartY=0.736122 StartZ=0 EndX=-1.275 EndY=-0.736122 EndZ=0
    g3: LineSegment StartX=-1.275 StartY=-0.736122 StartZ=0 EndX=1.34766e-11 EndY=-1.47224 EndZ=0
    g4: LineSegment StartX=1.34766e-11 StartY=-1.47224 StartZ=0 EndX=1.275 EndY=-0.736122 EndZ=0
    g5: LineSegment StartX=1.275 StartY=-0.736122 StartZ=0 EndX=1.275 EndY=0.736122 EndZ=0
    g6: Circle [constr] CenterX=0 CenterY=0 CenterZ=0 NormalX=0 NormalY=0 NormalZ=1 AngleXU=0 Radius=1.47224
  constraints (16):
    c: Coincident(g0,g1)
    c: Coincident(g1,g2)
    c: Coincident(g2,g3)
    c: Coincident(g3,g4)
    c: Coincident(g4,g5)
    c: Coincident(g5,g0)
    c: Equal(g0, g1-g5) x5
    c: PointOnObject(g0,g6)
    c: PointOnObject(g1,g6)
    c: PointOnObject(g2,g6)
    c: PointOnObject(g3,g6)
    c: PointOnObject(g4,g6)
    c: PointOnObject(g5,g6)
    c: Coincident(g6,g-1)
    c: PointOnObject(g0,g-2)
    c: DistanceX(g1,g0) = 2.55
FEATURE [PartDesign::Pocket] Pocket636  label="M3x20 Wrench070"
  BaseFeature = -> Pad662
  Length = 1.3
  Length2 = 100
  Profile = -> Sketch1632
  Type = 0
FEATURE [PartDesign::Chamfer] Chamfer320  label="M3x20 Smooth060"
  Base = -> Pocket636 [Face11,Edge2,Edge24,Edge3]
  BaseFeature = -> Pocket636
  Size = 0.2
FEATURE [Sketcher::SketchObject] Sketch1803
  MapMode = 5
  Placement = pos=(0,0,0) rot=(1,0,0;3.14159rad)
  Support = -> [Pad750]
  sketch-geometry (7):
    g0: LineSegment StartX=1.275 StartY=0.736122 StartZ=0 EndX=0 EndY=1.47224 EndZ=0
    g1: LineSegment StartX=0 StartY=1.47224 StartZ=0 EndX=-1.275 EndY=0.736122 EndZ=0
    g2: LineSegment StartX=-1.275 StartY=0.736122 StartZ=0 EndX=-1.275 EndY=-0.736122 EndZ=0
    g3: LineSegment StartX=-1.275 StartY=-0.736122 StartZ=0 EndX=1.34766e-11 EndY=-1.47224 EndZ=0
    g4: LineSegment StartX=1.34766e-11 StartY=-1.47224 StartZ=0 EndX=1.275 EndY=-0.736122 EndZ=0
    g5: LineSegment StartX=1.275 StartY=-0.736122 StartZ=0 EndX=1.275 EndY=0.736122 EndZ=0
    g6: Circle [constr] CenterX=0 CenterY=0 CenterZ=0 NormalX=0 NormalY=0 NormalZ=1 AngleXU=0 Radius=1.47224
  constraints (16):
    c: Coincident(g0,g1)
    c: Coincident(g1,g2)
    c: Coincident(g2,g3)
    c: Coincident(g3,g4)
    c: Coincident(g4,g5)
    c: Coincident(g5,g0)
    c: Equal(g0, g1-g5) x5
    c: PointOnObject(g0,g6)
    c: PointOnObject(g1,g6)
    c: PointOnObject(g2,g6)
    c: PointOnObject(g3,g6)
    c: PointOnObject(g4,g6)
    c: PointOnObject(g5,g6)
    c: Coincident(g6,g-1)
    c: PointOnObject(g0,g-2)
    c: DistanceX(g1,g0) = 2.55
FEATURE [PartDesign::Pocket] Pocket582  label="M3x20 Wrench061"
  BaseFeature = -> Pad750
  Length = 1.3
  Length2 = 100
  Profile = -> Sketch1803
  Type = 0
FEATURE [PartDesign::Chamfer] Chamfer362  label="M3x20 Smooth069"
  Base = -> Pocket582 [Face11,Edge2,Edge24,Edge3]
  BaseFeature = -> Pocket582
  Size = 0.2
FEATURE [Sketcher::SketchObject] Sketch1804
  MapMode = 5
  Support = -> [XY_Plane670]
  sketch-geometry (1):
    g0: Circle CenterX=0 CenterY=0 CenterZ=0 NormalX=0 NormalY=0 NormalZ=1 AngleXU=0 Radius=2.75
  constraints (2):
    c: Coincident(g0,g-1)
    c: Radius(g0) = 2.75
FEATURE [PartDesign::Pad] Pad656  label="M3x20 Head057"
  Length = 3
  Length2 = 100
  Profile = -> Sketch1804
  Type = 0
FEATURE [Sketcher::SketchObject] Sketch1784
  MapMode = 5
  Placement = pos=(0,0,3) rot=(0,0,1;0rad)
  Support = -> [Pad656]
  sketch-geometry (1):
    g0: Circle CenterX=0 CenterY=0 CenterZ=0 NormalX=0 NormalY=0 NormalZ=1 AngleXU=0 Radius=1.5
  constraints (2):
    c: Coincident(g0,g-1)
    c: Radius(g0) = 1.5
FEATURE [PartDesign::Pad] Pad655  label="M3x20 Thread056"
  BaseFeature = -> Pad656
  Length = 20
  Length2 = 100
  Profile = -> Sketch1784
  Type = 0
FEATURE [Sketcher::SketchObject] Sketch1797
  MapMode = 5
  Placement = pos=(0,0,0) rot=(1,0,0;3.14159rad)
  Support = -> [Pad655]
  sketch-geometry (7):
    g0: LineSegment StartX=1.275 StartY=0.736122 StartZ=0 EndX=0 EndY=1.47224 EndZ=0
    g1: LineSegment StartX=0 StartY=1.47224 StartZ=0 EndX=-1.275 EndY=0.736122 EndZ=0
    g2: LineSegment StartX=-1.275 StartY=0.736122 StartZ=0 EndX=-1.275 EndY=-0.736122 EndZ=0
    g3: LineSegment StartX=-1.275 StartY=-0.736122 StartZ=0 EndX=1.34766e-11 EndY=-1.47224 EndZ=0
    g4: LineSegment StartX=1.34766e-11 StartY=-1.47224 StartZ=0 EndX=1.275 EndY=-0.736122 EndZ=0
    g5: LineSegment StartX=1.275 StartY=-0.736122 StartZ=0 EndX=1.275 EndY=0.736122 EndZ=0
    g6: Circle [constr] CenterX=0 CenterY=0 CenterZ=0 NormalX=0 NormalY=0 NormalZ=1 AngleXU=0 Radius=1.47224
  constraints (16):
    c: Coincident(g0,g1)
    c: Coincident(g1,g2)
    c: Coincident(g2,g3)
    c: Coincident(g3,g4)
    c: Coincident(g4,g5)
    c: Coincident(g5,g0)
    c: Equal(g0, g1-g5) x5
    c: PointOnObject(g0,g6)
    c: PointOnObject(g1,g6)
    c: PointOnObject(g2,g6)
    c: PointOnObject(g3,g6)
    c: PointOnObject(g4,g6)
    c: PointOnObject(g5,g6)
    c: Coincident(g6,g-1)
    c: PointOnObject(g0,g-2)
    c: DistanceX(g1,g0) = 2.55
FEATURE [PartDesign::Pocket] Pocket565  label="M3x20 Wrench056"
  BaseFeature = -> Pad655
  Length = 1.3
  Length2 = 100
  Profile = -> Sketch1797
  Type = 0
FEATURE [PartDesign::Chamfer] Chamfer325  label="M3x20 Smooth061"
  Base = -> Pocket565 [Face11,Edge2,Edge24,Edge3]
  BaseFeature = -> Pocket565
  Size = 0.2
FEATURE [Sketcher::SketchObject] Sketch1807
  MapMode = 5
  Placement = pos=(0,0,0) rot=(0.57735,0.57735,0.57735;2.0944rad)
  Support = -> [YZ_Plane599]
  sketch-geometry (4):
    g0: LineSegment StartX=35.5 StartY=17.1 StartZ=0 EndX=38.5 EndY=17.1 EndZ=0
    g1: LineSegment StartX=38.5 StartY=17.1 StartZ=0 EndX=38.5 EndY=22.9 EndZ=0
    g2: LineSegment StartX=38.5 StartY=22.9 StartZ=0 EndX=35.5 EndY=22.9 EndZ=0
    g3: LineSegment StartX=35.5 StartY=22.9 StartZ=0 EndX=35.5 EndY=17.1 EndZ=0
  constraints (12):
    c: Coincident(g0,g1)
    c: Coincident(g1,g2)
    c: Coincident(g2,g3)
    c: Coincident(g3,g0)
    c: Horizontal(g0)
    c: Horizontal(g2)
    c: Vertical(g1)
    c: Vertical(g3)
    c: DistanceX(g2,g2) = 3
    c: DistanceY(g1,g1) = 5.8
    c: DistanceX(g-1,g0) = 38.5
    c: DistanceY(g-1,g0) = 17.1
FEATURE [Sketcher::SketchObject] Sketch1810
  MapMode = 5
  Support = -> [XY_Plane618]
  sketch-geometry (8):
    g0: LineSegment StartX=0 StartY=3.17543 StartZ=0 EndX=-2.75 EndY=1.58771 EndZ=0
    g1: LineSegment StartX=-2.75 StartY=1.58771 StartZ=0 EndX=-2.75 EndY=-1.58771 EndZ=0
    g2: LineSegment StartX=-2.75 StartY=-1.58771 StartZ=0 EndX=0 EndY=-3.17543 EndZ=0
    g3: LineSegment StartX=0 StartY=-3.17543 StartZ=0 EndX=2.75 EndY=-1.58771 EndZ=0
    g4: LineSegment StartX=2.75 StartY=-1.58771 StartZ=0 EndX=2.75 EndY=1.58771 EndZ=0
    g5: LineSegment StartX=2.75 StartY=1.58771 StartZ=0 EndX=0 EndY=3.17543 EndZ=0
    g6: Circle [constr] CenterX=0 CenterY=0 CenterZ=0 NormalX=0 NormalY=0 NormalZ=1 AngleXU=0 Radius=3.17543
    g7: Circle CenterX=0 CenterY=0 CenterZ=0 NormalX=0 NormalY=0 NormalZ=1 AngleXU=0 Radius=1.5
  constraints (18):
    c: Coincident(g0,g1)
    c: Coincident(g1,g2)
    c: Coincident(g2,g3)
    c: Coincident(g3,g4)
    c: Coincident(g4,g5)
    c: Coincident(g5,g0)
    c: Equal(g0, g1-g5) x5
    c: PointOnObject(g0,g6)
    c: PointOnObject(g1,g6)
    c: PointOnObject(g2,g6)
    c: PointOnObject(g3,g6)
    c: PointOnObject(g4,g6)
    c: PointOnObject(g5,g6)
    c: Coincident(g6,g-1)
    c: PointOnObject(g5,g-2)
    c: DistanceX(g0,g4) = 5.5
    c: Coincident(g7,g-1)
    c: Radius(g7) = 1.5
FEATURE [PartDesign::Pad] Pad754  label="M3 Nut Primitive144"
  Length = 1.2
  Length2 = 1.2
  Profile = -> Sketch1810
  Type = 4
FEATURE [Sketcher::SketchObject] Sketch1616
  ExternalGeometry = -> [Pad754]
  MapMode = 5
  Placement = pos=(0,0,0) rot=(0.57735,0.57735,0.57735;2.0944rad)
  Support = -> [YZ_Plane598]
  sketch-geometry (6):
    g0: LineSegment StartX=-2.67543 StartY=1.2 StartZ=0 EndX=-3.67543 EndY=1.2 EndZ=0
    g1: LineSegment StartX=-3.67543 StartY=1.2 StartZ=0 EndX=-3.67543 EndY=-1.2 EndZ=0
    g2: LineSegment StartX=-3.67543 StartY=-1.2 StartZ=0 EndX=-2.67543 EndY=-1.2 EndZ=0
    g3: LineSegment StartX=-2.67543 StartY=-1.2 StartZ=0 EndX=-3.17543 EndY=-1 EndZ=0
    g4: LineSegment StartX=-3.17543 StartY=-1 StartZ=0 EndX=-3.17543 EndY=1 EndZ=0
    g5: LineSegment StartX=-3.17543 StartY=1 StartZ=0 EndX=-2.67543 EndY=1.2 EndZ=0
  constraints (15):
    c: Horizontal(g0)
    c: Coincident(g0,g1)
    c: Coincident(g1,g2)
    c: Coincident(g2,g3)
    c: Coincident(g3,g4)
    c: Coincident(g4,g5)
    c: Coincident(g5,g0)
    c: Symmetric(g4,g3,g-1)
    c: Symmetric(g0,g2,g-1)
    c: Symmetric(g1,g0,g-1)
    c: DistanceX(g0,g4) = 0.5
    c: DistanceY(g3,g4) = 2
    c: DistanceY(g1,g0) = 2.4
    c: PointOnObject(g3,g-3)
    c: DistanceX(g4,g0) = 0.5
FEATURE [Sketcher::SketchObject] Sketch1815
  MapMode = 5
  Support = -> [XY_Plane595]
  sketch-geometry (12):
    g0: LineSegment StartX=0 StartY=0 StartZ=0 EndX=0 EndY=57 EndZ=0
    g1: LineSegment StartX=0 StartY=57 StartZ=0 EndX=40 EndY=57 EndZ=0
    g2: ArcOfCircle CenterX=40 CenterY=44.5 CenterZ=0 NormalX=0 NormalY=0 NormalZ=1 AngleXU=0 Radius=12.5 StartAngle=0.643501 EndAngle=1.5708
    g3: ArcOfCircle CenterX=60 CenterY=59.5 CenterZ=0 NormalX=0 NormalY=0 NormalZ=1 AngleXU=0 Radius=12.5 StartAngle=3.78509 EndAngle=4.71239
    g4: LineSegment StartX=60 StartY=47 StartZ=0 EndX=120 EndY=47 EndZ=0
    g5: ArcOfCircle CenterX=120 CenterY=37 CenterZ=0 NormalX=0 NormalY=0 NormalZ=1 AngleXU=0 Radius=10 StartAngle=2e-16 EndAngle=1.5708
    g6: LineSegment StartX=130 StartY=37 StartZ=0 EndX=130 EndY=15 EndZ=0
    g7: ArcOfCircle CenterX=125 CenterY=15 CenterZ=0 NormalX=0 NormalY=0 NormalZ=1 AngleXU=0 Radius=5 StartAngle=4.71239 EndAngle=6.28319
    g8: LineSegment StartX=125 StartY=10 StartZ=0 EndX=60 EndY=10 EndZ=0
    g9: LineSegment StartX=40 StartY=0 StartZ=0 EndX=0 EndY=0 EndZ=0
    g10: ArcOfCircle CenterX=40 CenterY=12.5 CenterZ=0 NormalX=0 NormalY=0 NormalZ=1 AngleXU=0 Radius=12.5 StartAngle=4.71239 EndAngle=5.63968
    g11: ArcOfCircle CenterX=60 CenterY=-2.5 CenterZ=0 NormalX=0 NormalY=0 NormalZ=1 AngleXU=0 Radius=12.5 StartAngle=1.5708 EndAngle=2.49809
  constraints (31):
    c: Coincident(g-1,g0)
    c: PointOnObject(g0,g-2)
    c: Coincident(g0,g1)
    c: Horizontal(g1)
    c: Tangent(g1,g2) = 1.5708
    c: Tangent(g2,g3) = 1.5708
    c: Tangent(g3,g4) = -1.5708
    c: Tangent(g4,g5) = 1.5708
    c: Tangent(g5,g6) = 1.5708
    c: Tangent(g6,g7) = 1.5708
    c: Tangent(g7,g8) = 1.5708
    c: Coincident(g9,g0)
    c: Horizontal(g9)
    c: Horizontal(g4)
    c: Horizontal(g8)
    c: Vertical(g6)
    c: Tangent(g11,g8) = -1.5708
    c: Tangent(g11,g10) = 1.5708
    c: Radius(g7) = 5
    c: Radius(g5) = 10
    c: DistanceX(g1,g1) = 40
    c: DistanceX(g0,g6) = 130
    c: DistanceX(g1,g3) = 20
    c: Tangent(g10,g9) = 1.5708
    c: DistanceX(g9,g8) = 20
    c: DistanceX(g9,g9) = 40
    c: DistanceY(g0,g0) = 57
    c: DistanceY(g9,g8) = 10
    c: DistanceY(g3,g1) = 10
    c: DistanceX(g10,g8) = 10
    c: DistanceX(g2,g3) = 10
FEATURE [Sketcher::SketchObject] Sketch1816
  MapMode = 5
  Placement = pos=(0,0,0) rot=(1,0,0;1.5708rad)
  Support = -> [XZ_Plane595]
  sketch-geometry (4):
    g0: LineSegment StartX=68.5 StartY=25 StartZ=0 EndX=125 EndY=25 EndZ=0
    g1: LineSegment StartX=125 StartY=25 StartZ=0 EndX=125 EndY=5 EndZ=0
    g2: LineSegment StartX=125 StartY=5 StartZ=0 EndX=68.5 EndY=5 EndZ=0
    g3: LineSegment StartX=68.5 StartY=5 StartZ=0 EndX=68.5 EndY=25 EndZ=0
  constraints (12):
    c: Coincident(g0,g1)
    c: Coincident(g1,g2)
    c: Coincident(g2,g3)
    c: Coincident(g3,g0)
    c: Horizontal(g0)
    c: Horizontal(g2)
    c: Vertical(g1)
    c: Vertical(g3)
    c: DistanceX(g0,g0) = 56.5
    c: DistanceY(g3,g3) = 20
    c: DistanceY(g-1,g2) = 5
    c: DistanceX(g-1,g0) = 68.5
FEATURE [Sketcher::SketchObject] Sketch1820
  MapMode = 5
  Support = -> [XY_Plane607]
  sketch-geometry (8):
    g0: LineSegment StartX=0 StartY=3.17543 StartZ=0 EndX=-2.75 EndY=1.58771 EndZ=0
    g1: LineSegment StartX=-2.75 StartY=1.58771 StartZ=0 EndX=-2.75 EndY=-1.58771 EndZ=0
    g2: LineSegment StartX=-2.75 StartY=-1.58771 StartZ=0 EndX=0 EndY=-3.17543 EndZ=0
    g3: LineSegment StartX=0 StartY=-3.17543 StartZ=0 EndX=2.75 EndY=-1.58771 EndZ=0
    g4: LineSegment StartX=2.75 StartY=-1.58771 StartZ=0 EndX=2.75 EndY=1.58771 EndZ=0
    g5: LineSegment StartX=2.75 StartY=1.58771 StartZ=0 EndX=0 EndY=3.17543 EndZ=0
    g6: Circle [constr] CenterX=0 CenterY=0 CenterZ=0 NormalX=0 NormalY=0 NormalZ=1 AngleXU=0 Radius=3.17543
    g7: Circle CenterX=0 CenterY=0 CenterZ=0 NormalX=0 NormalY=0 NormalZ=1 AngleXU=0 Radius=1.5
  constraints (18):
    c: Coincident(g0,g1)
    c: Coincident(g1,g2)
    c: Coincident(g2,g3)
    c: Coincident(g3,g4)
    c: Coincident(g4,g5)
    c: Coincident(g5,g0)
    c: Equal(g0, g1-g5) x5
    c: PointOnObject(g0,g6)
    c: PointOnObject(g1,g6)
    c: PointOnObject(g2,g6)
    c: PointOnObject(g3,g6)
    c: PointOnObject(g4,g6)
    c: PointOnObject(g5,g6)
    c: Coincident(g6,g-1)
    c: PointOnObject(g5,g-2)
    c: DistanceX(g0,g4) = 5.5
    c: Coincident(g7,g-1)
    c: Radius(g7) = 1.5
FEATURE [Sketcher::SketchObject] Sketch1823
  MapMode = 5
  Placement = pos=(0,0,0) rot=(0.57735,0.57735,0.57735;2.0944rad)
  Support = -> [YZ_Plane596]
  sketch-geometry (4):
    g0: LineSegment StartX=18.5 StartY=17.1 StartZ=0 EndX=21.5 EndY=17.1 EndZ=0
    g1: LineSegment StartX=21.5 StartY=17.1 StartZ=0 EndX=21.5 EndY=22.9 EndZ=0
    g2: LineSegment StartX=21.5 StartY=22.9 StartZ=0 EndX=18.5 EndY=22.9 EndZ=0
    g3: LineSegment StartX=18.5 StartY=22.9 StartZ=0 EndX=18.5 EndY=17.1 EndZ=0
  constraints (12):
    c: Coincident(g0,g1)
    c: Coincident(g1,g2)
    c: Coincident(g2,g3)
    c: Coincident(g3,g0)
    c: Horizontal(g0)
    c: Horizontal(g2)
    c: Vertical(g1)
    c: Vertical(g3)
    c: DistanceX(g2,g2) = 3
    c: DistanceY(g1,g1) = 5.8
    c: DistanceX(g-1,g0) = 21.5
    c: DistanceY(g-1,g0) = 17.1
FEATURE [Sketcher::SketchObject] Sketch1825
  MapMode = 5
  Support = -> [XY_Plane598]
  sketch-geometry (1):
    g0: Circle CenterX=0 CenterY=0 CenterZ=0 NormalX=0 NormalY=0 NormalZ=1 AngleXU=0 Radius=8
  constraints (2):
    c: Coincident(g0,g-1)
    c: Radius(g0) = 8
FEATURE [Sketcher::SketchObject] Sketch1826
  MapMode = 5
  Placement = pos=(0,0,0) rot=(1,0,0;1.5708rad)
  Support = -> [XZ_Plane598]
  sketch-geometry (4):
    g0: LineSegment StartX=68.5 StartY=25 StartZ=0 EndX=125 EndY=25 EndZ=0
    g1: LineSegment StartX=125 StartY=25 StartZ=0 EndX=125 EndY=5 EndZ=0
    g2: LineSegment StartX=125 StartY=5 StartZ=0 EndX=68.5 EndY=5 EndZ=0
    g3: LineSegment StartX=68.5 StartY=5 StartZ=0 EndX=68.5 EndY=25 EndZ=0
  constraints (12):
    c: Coincident(g0,g1)
    c: Coincident(g1,g2)
    c: Coincident(g2,g3)
    c: Coincident(g3,g0)
    c: Horizontal(g0)
    c: Horizontal(g2)
    c: Vertical(g1)
    c: Vertical(g3)
    c: DistanceX(g0,g0) = 56.5
    c: DistanceY(g3,g3) = 20
    c: DistanceY(g-1,g2) = 5
    c: DistanceX(g-1,g0) = 68.5
FEATURE [Sketcher::SketchObject] Sketch1864
  MapMode = 5
  Placement = pos=(0,0,0) rot=(1,0,0;1.5708rad)
  Support = -> [XZ_Plane643]
  sketch-geometry (8):
    g0: LineSegment StartX=-1.5 StartY=2.25 StartZ=0 EndX=-3.25 EndY=2.25 EndZ=0
    g1: LineSegment StartX=-3.25 StartY=2.25 StartZ=0 EndX=-3.25 EndY=1.25 EndZ=0
    g2: LineSegment StartX=-3.25 StartY=1.25 StartZ=0 EndX=-2 EndY=1.25 EndZ=0
    g3: LineSegment StartX=-2 StartY=1.25 StartZ=0 EndX=-2 EndY=-1.25 EndZ=0
    g4: LineSegment StartX=-2 StartY=-1.25 StartZ=0 EndX=-3.25 EndY=-1.25 EndZ=0
    g5: LineSegment StartX=-3.25 StartY=-1.25 StartZ=0 EndX=-3.25 EndY=-2.25 EndZ=0
    g6: LineSegment StartX=-3.25 StartY=-2.25 StartZ=0 EndX=-1.5 EndY=-2.25 EndZ=0
    g7: LineSegment StartX=-1.5 StartY=-2.25 StartZ=0 EndX=-1.5 EndY=2.25 EndZ=0
  constraints (23):
    c: Horizontal(g0)
    c: Coincident(g0,g1)
    c: Vertical(g1)
    c: Coincident(g1,g2)
    c: Horizontal(g2)
    c: Coincident(g2,g3)
    c: Vertical(g3)
    c: Coincident(g3,g4)
    c: Horizontal(g4)
    c: Coincident(g4,g5)
    c: Vertical(g5)
    c: Coincident(g5,g6)
    c: Horizontal(g6)
    c: Coincident(g6,g7)
    c: Vertical(g7)
    c: Coincident(g0,g7)
    c: Equal(g1,g5)
    c: Symmetric(g4,g1,g-1)
    c: DistanceX(g0,g-1) = 1.5
    c: DistanceY(g3,g3) = 2.5
    c: DistanceY(g7,g7) = 4.5
    c: DistanceX(g0,g-1) = 3.25
    c: DistanceX(g2,g-1) = 2
FEATURE [PartDesign::Revolution] Revolution038
  Angle = 360
  Axis = (0,2e-16,1)
  Base = (0,0,0)
  Placement = pos=(0,0,0) rot=(1,0,0;1.5708rad)
  Profile = -> Sketch1864
  ReferenceAxis = -> Sketch1864 [V_Axis]
FEATURE [PartDesign::Fillet] Fillet209
  Base = -> Revolution038 [Face2,Face6,Edge1,Edge11,Face4]
  BaseFeature = -> Revolution038
  Placement = pos=(0,0,0) rot=(1,0,0;1.5708rad)
  Radius = 0.25
FEATURE [Sketcher::SketchObject] Sketch1866
  MapMode = 5
  Placement = pos=(0,0,0) rot=(1,0,0;1.5708rad)
  Support = -> [XZ_Plane730]
  sketch-geometry (8):
    g0: LineSegment StartX=-1.5 StartY=2.25 StartZ=0 EndX=-3.25 EndY=2.25 EndZ=0
    g1: LineSegment StartX=-3.25 StartY=2.25 StartZ=0 EndX=-3.25 EndY=1.25 EndZ=0
    g2: LineSegment StartX=-3.25 StartY=1.25 StartZ=0 EndX=-2 EndY=1.25 EndZ=0
    g3: LineSegment StartX=-2 StartY=1.25 StartZ=0 EndX=-2 EndY=-1.25 EndZ=0
    g4: LineSegment StartX=-2 StartY=-1.25 StartZ=0 EndX=-3.25 EndY=-1.25 EndZ=0
    g5: LineSegment StartX=-3.25 StartY=-1.25 StartZ=0 EndX=-3.25 EndY=-2.25 EndZ=0
    g6: LineSegment StartX=-3.25 StartY=-2.25 StartZ=0 EndX=-1.5 EndY=-2.25 EndZ=0
    g7: LineSegment StartX=-1.5 StartY=-2.25 StartZ=0 EndX=-1.5 EndY=2.25 EndZ=0
  constraints (23):
    c: Horizontal(g0)
    c: Coincident(g0,g1)
    c: Vertical(g1)
    c: Coincident(g1,g2)
    c: Horizontal(g2)
    c: Coincident(g2,g3)
    c: Vertical(g3)
    c: Coincident(g3,g4)
    c: Horizontal(g4)
    c: Coincident(g4,g5)
    c: Vertical(g5)
    c: Coincident(g5,g6)
    c: Horizontal(g6)
    c: Coincident(g6,g7)
    c: Vertical(g7)
    c: Coincident(g0,g7)
    c: Equal(g1,g5)
    c: Symmetric(g4,g1,g-1)
    c: DistanceX(g0,g-1) = 1.5
    c: DistanceY(g3,g3) = 2.5
    c: DistanceY(g7,g7) = 4.5
    c: DistanceX(g0,g-1) = 3.25
    c: DistanceX(g2,g-1) = 2
FEATURE [PartDesign::Revolution] Revolution036
  Angle = 360
  Axis = (0,2e-16,1)
  Base = (0,0,0)
  Placement = pos=(0,0,0) rot=(1,0,0;1.5708rad)
  Profile = -> Sketch1866
  ReferenceAxis = -> Sketch1866 [V_Axis]
FEATURE [PartDesign::Fillet] Fillet215
  Base = -> Revolution036 [Face2,Face6,Edge1,Edge11,Face4]
  BaseFeature = -> Revolution036
  Placement = pos=(0,0,0) rot=(1,0,0;1.5708rad)
  Radius = 0.25
FEATURE [Sketcher::SketchObject] Sketch1869
  MapMode = 5
  Placement = pos=(0,0,0) rot=(1,0,0;1.5708rad)
  Support = -> [XZ_Plane733]
  sketch-geometry (8):
    g0: LineSegment StartX=-1.5 StartY=2.25 StartZ=0 EndX=-3.25 EndY=2.25 EndZ=0
    g1: LineSegment StartX=-3.25 StartY=2.25 StartZ=0 EndX=-3.25 EndY=1.25 EndZ=0
    g2: LineSegment StartX=-3.25 StartY=1.25 StartZ=0 EndX=-2 EndY=1.25 EndZ=0
    g3: LineSegment StartX=-2 StartY=1.25 StartZ=0 EndX=-2 EndY=-1.25 EndZ=0
    g4: LineSegment StartX=-2 StartY=-1.25 StartZ=0 EndX=-3.25 EndY=-1.25 EndZ=0
    g5: LineSegment StartX=-3.25 StartY=-1.25 StartZ=0 EndX=-3.25 EndY=-2.25 EndZ=0
    g6: LineSegment StartX=-3.25 StartY=-2.25 StartZ=0 EndX=-1.5 EndY=-2.25 EndZ=0
    g7: LineSegment StartX=-1.5 StartY=-2.25 StartZ=0 EndX=-1.5 EndY=2.25 EndZ=0
  constraints (23):
    c: Horizontal(g0)
    c: Coincident(g0,g1)
    c: Vertical(g1)
    c: Coincident(g1,g2)
    c: Horizontal(g2)
    c: Coincident(g2,g3)
    c: Vertical(g3)
    c: Coincident(g3,g4)
    c: Horizontal(g4)
    c: Coincident(g4,g5)
    c: Vertical(g5)
    c: Coincident(g5,g6)
    c: Horizontal(g6)
    c: Coincident(g6,g7)
    c: Vertical(g7)
    c: Coincident(g0,g7)
    c: Equal(g1,g5)
    c: Symmetric(g4,g1,g-1)
    c: DistanceX(g0,g-1) = 1.5
    c: DistanceY(g3,g3) = 2.5
    c: DistanceY(g7,g7) = 4.5
    c: DistanceX(g0,g-1) = 3.25
    c: DistanceX(g2,g-1) = 2
FEATURE [PartDesign::Revolution] Revolution046
  Angle = 360
  Axis = (0,2e-16,1)
  Base = (0,0,0)
  Placement = pos=(0,0,0) rot=(1,0,0;1.5708rad)
  Profile = -> Sketch1869
  ReferenceAxis = -> Sketch1869 [V_Axis]
FEATURE [PartDesign::Fillet] Fillet217
  Base = -> Revolution046 [Face2,Face6,Edge1,Edge11,Face4]
  BaseFeature = -> Revolution046
  Placement = pos=(0,0,0) rot=(1,0,0;1.5708rad)
  Radius = 0.25
FEATURE [Sketcher::SketchObject] Sketch1871
  MapMode = 5
  Placement = pos=(0,0,0) rot=(1,0,0;1.5708rad)
  Support = -> [XZ_Plane693]
  sketch-geometry (8):
    g0: LineSegment StartX=-1.5 StartY=2.25 StartZ=0 EndX=-3.25 EndY=2.25 EndZ=0
    g1: LineSegment StartX=-3.25 StartY=2.25 StartZ=0 EndX=-3.25 EndY=1.25 EndZ=0
    g2: LineSegment StartX=-3.25 StartY=1.25 StartZ=0 EndX=-2 EndY=1.25 EndZ=0
    g3: LineSegment StartX=-2 StartY=1.25 StartZ=0 EndX=-2 EndY=-1.25 EndZ=0
    g4: LineSegment StartX=-2 StartY=-1.25 StartZ=0 EndX=-3.25 EndY=-1.25 EndZ=0
    g5: LineSegment StartX=-3.25 StartY=-1.25 StartZ=0 EndX=-3.25 EndY=-2.25 EndZ=0
    g6: LineSegment StartX=-3.25 StartY=-2.25 StartZ=0 EndX=-1.5 EndY=-2.25 EndZ=0
    g7: LineSegment StartX=-1.5 StartY=-2.25 StartZ=0 EndX=-1.5 EndY=2.25 EndZ=0
  constraints (23):
    c: Horizontal(g0)
    c: Coincident(g0,g1)
    c: Vertical(g1)
    c: Coincident(g1,g2)
    c: Horizontal(g2)
    c: Coincident(g2,g3)
    c: Vertical(g3)
    c: Coincident(g3,g4)
    c: Horizontal(g4)
    c: Coincident(g4,g5)
    c: Vertical(g5)
    c: Coincident(g5,g6)
    c: Horizontal(g6)
    c: Coincident(g6,g7)
    c: Vertical(g7)
    c: Coincident(g0,g7)
    c: Equal(g1,g5)
    c: Symmetric(g4,g1,g-1)
    c: DistanceX(g0,g-1) = 1.5
    c: DistanceY(g3,g3) = 2.5
    c: DistanceY(g7,g7) = 4.5
    c: DistanceX(g0,g-1) = 3.25
    c: DistanceX(g2,g-1) = 2
FEATURE [PartDesign::Revolution] Revolution042
  Angle = 360
  Axis = (0,2e-16,1)
  Base = (0,0,0)
  Placement = pos=(0,0,0) rot=(1,0,0;1.5708rad)
  Profile = -> Sketch1871
  ReferenceAxis = -> Sketch1871 [V_Axis]
FEATURE [PartDesign::Fillet] Fillet202
  Base = -> Revolution042 [Face2,Face6,Edge1,Edge11,Face4]
  BaseFeature = -> Revolution042
  Placement = pos=(0,0,0) rot=(1,0,0;1.5708rad)
  Radius = 0.25
FEATURE [Sketcher::SketchObject] Sketch1892
  ExternalGeometry = -> [Pad707]
  MapMode = 5
  Placement = pos=(0,0,0) rot=(0.57735,0.57735,0.57735;2.0944rad)
  Support = -> [YZ_Plane584]
  sketch-geometry (6):
    g0: LineSegment StartX=-1.9594 StartY=0.6 StartZ=0 EndX=-2.8094 EndY=0.6 EndZ=0
    g1: LineSegment StartX=-2.8094 StartY=0.6 StartZ=0 EndX=-2.8094 EndY=-0.6 EndZ=0
    g2: LineSegment StartX=-2.8094 StartY=-0.6 StartZ=0 EndX=-1.9594 EndY=-0.6 EndZ=0
    g3: LineSegment StartX=-1.9594 StartY=-0.6 StartZ=0 EndX=-2.3094 EndY=-0.4 EndZ=0
    g4: LineSegment StartX=-2.3094 StartY=-0.4 StartZ=0 EndX=-2.3094 EndY=0.4 EndZ=0
    g5: LineSegment StartX=-2.3094 StartY=0.4 StartZ=0 EndX=-1.9594 EndY=0.6 EndZ=0
  constraints (15):
    c: Horizontal(g0)
    c: Coincident(g0,g1)
    c: Coincident(g1,g2)
    c: Coincident(g2,g3)
    c: Coincident(g3,g4)
    c: Coincident(g4,g5)
    c: Coincident(g5,g0)
    c: Symmetric(g4,g3,g-1)
    c: Symmetric(g0,g2,g-1)
    c: Symmetric(g1,g0,g-1)
    c: DistanceX(g0,g4) = 0.5
    c: DistanceY(g3,g4) = 0.8
    c: DistanceY(g1,g0) = 1.2
    c: PointOnObject(g3,g-3)
    c: DistanceX(g4,g0) = 0.35
FEATURE [PartDesign::Groove] Groove144  label="M3 Nut Smooth136"
  Angle = 360
  Axis = (-2e-16,3e-16,1)
  Base = (0,0,0)
  BaseFeature = -> Pad707
  Profile = -> Sketch1892
  ReferenceAxis = -> Sketch1892 [V_Axis]
  Reversed = true
FEATURE [PartDesign::Chamfer] Chamfer335  label="M3 Nut Smooth Hole141"
  Base = -> Groove144 [Edge24,Edge23]
  BaseFeature = -> Groove144
  Size = 0.2
FEATURE [Sketcher::SketchObject] Sketch1901
  MapMode = 5
  Placement = pos=(0,0,2) rot=(0,0,1;0rad)
  Support = -> [Pad693]
  sketch-geometry (1):
    g0: Circle CenterX=0 CenterY=0 CenterZ=0 NormalX=0 NormalY=0 NormalZ=1 AngleXU=0 Radius=1
  constraints (2):
    c: Coincident(g0,g-1)
    c: Radius(g0) = 1
FEATURE [PartDesign::Pad] Pad699  label="M3x8 Thread086"
  BaseFeature = -> Pad693
  Length = 8
  Length2 = 100
  Profile = -> Sketch1901
  Type = 0
FEATURE [Sketcher::SketchObject] Sketch1531
  MapMode = 5
  Placement = pos=(0,0,0) rot=(1,0,0;3.14159rad)
  Support = -> [Pad699]
  sketch-geometry (7):
    g0: LineSegment StartX=0.77 StartY=0.44456 StartZ=0 EndX=0 EndY=0.889119 EndZ=0
    g1: LineSegment StartX=0 StartY=0.889119 StartZ=0 EndX=-0.77 EndY=0.44456 EndZ=0
    g2: LineSegment StartX=-0.77 StartY=0.44456 StartZ=0 EndX=-0.77 EndY=-0.44456 EndZ=0
    g3: LineSegment StartX=-0.77 StartY=-0.44456 StartZ=0 EndX=3.85628e-11 EndY=-0.889119 EndZ=0
    g4: LineSegment StartX=3.85628e-11 StartY=-0.889119 StartZ=0 EndX=0.77 EndY=-0.44456 EndZ=0
    g5: LineSegment StartX=0.77 StartY=-0.44456 StartZ=0 EndX=0.77 EndY=0.44456 EndZ=0
    g6: Circle [constr] CenterX=0 CenterY=0 CenterZ=0 NormalX=0 NormalY=0 NormalZ=1 AngleXU=0 Radius=0.889119
  constraints (16):
    c: Coincident(g0,g1)
    c: Coincident(g1,g2)
    c: Coincident(g2,g3)
    c: Coincident(g3,g4)
    c: Coincident(g4,g5)
    c: Coincident(g5,g0)
    c: Equal(g0, g1-g5) x5
    c: PointOnObject(g0,g6)
    c: PointOnObject(g1,g6)
    c: PointOnObject(g2,g6)
    c: PointOnObject(g3,g6)
    c: PointOnObject(g4,g6)
    c: PointOnObject(g5,g6)
    c: Coincident(g6,g-1)
    c: PointOnObject(g0,g-2)
    c: DistanceX(g1,g0) = 1.54
FEATURE [PartDesign::Pocket] Pocket612  label="M3x8 Wrench090"
  BaseFeature = -> Pad699
  Length = 1
  Length2 = 100
  Profile = -> Sketch1531
  Type = 0
FEATURE [Sketcher::SketchObject] Sketch1902
  MapMode = 5
  Placement = pos=(0,0,25) rot=(0,0,1;0rad)
  Support = -> [Pocket606]
  sketch-geometry (5):
    g0: ArcOfCircle CenterX=22.5 CenterY=23.1875 CenterZ=0 NormalX=0 NormalY=0 NormalZ=1 AngleXU=0 Radius=45.1875 StartAngle=4.19118 EndAngle=4.71239
    g1: LineSegment StartX=22.5 StartY=-22 StartZ=0 EndX=56.5 EndY=-22 EndZ=0
    g2: LineSegment StartX=56.5 StartY=-22 StartZ=0 EndX=56.5 EndY=-23 EndZ=0
    g3: LineSegment StartX=56.5 StartY=-23 StartZ=0 EndX=0 EndY=-23 EndZ=0
    g4: LineSegment StartX=0 StartY=-23 StartZ=0 EndX=0 EndY=-16 EndZ=0
  constraints (15):
    c: PointOnObject(g0,g-2)
    c: Horizontal(g1)
    c: Coincident(g2,g1)
    c: Vertical(g2)
    c: Coincident(g3,g2)
    c: Horizontal(g3)
    c: Coincident(g4,g3)
    c: Coincident(g4,g0)
    c: Vertical(g4)
    c: Tangent(g1,g0) = -1.5708
    c: DistanceX(g0,g0) = 22.5
    c: DistanceY(g4,g4) = 7
    c: DistanceY(g2,g2) = 1
    c: DistanceY(g0,g-1) = 16
    c: DistanceX(g3,g3) = 56.5
FEATURE [PartDesign::Pocket] Pocket601  label="Swing Counterpart003"
  BaseFeature = -> Pocket606
  Length = 25
  Length2 = 100
  Profile = -> Sketch1902
  Type = 0
FEATURE [Sketcher::SketchObject] Sketch1529
  MapMode = 5
  Placement = pos=(56.5,0,0) rot=(0.57735,0.57735,0.57735;2.0944rad)
  Support = -> [Pocket601]
  sketch-geometry (8):
    g0: LineSegment StartX=-6 StartY=22.9 StartZ=0 EndX=-3 EndY=22.9 EndZ=0
    g1: LineSegment StartX=-3 StartY=22.9 StartZ=0 EndX=-3 EndY=17.1 EndZ=0
    g2: LineSegment StartX=-3 StartY=17.1 StartZ=0 EndX=-6 EndY=17.1 EndZ=0
    g3: LineSegment StartX=-6 StartY=17.1 StartZ=0 EndX=-6 EndY=22.9 EndZ=0
    g4: LineSegment StartX=-6 StartY=12.9 StartZ=0 EndX=-3 EndY=12.9 EndZ=0
    g5: LineSegment StartX=-3 StartY=12.9 StartZ=0 EndX=-3 EndY=7.1 EndZ=0
    g6: LineSegment StartX=-3 StartY=7.1 StartZ=0 EndX=-6 EndY=7.1 EndZ=0
    g7: LineSegment StartX=-6 StartY=7.1 StartZ=0 EndX=-6 EndY=12.9 EndZ=0
  constraints (24):
    c: Coincident(g0,g1)
    c: Coincident(g1,g2)
    c: Coincident(g2,g3)
    c: Coincident(g3,g0)
    c: Horizontal(g0)
    c: Horizontal(g2)
    c: Vertical(g1)
    c: Vertical(g3)
    c: Coincident(g4,g5)
    c: Coincident(g5,g6)
    c: Coincident(g6,g7)
    c: Coincident(g7,g4)
    c: Horizontal(g4)
    c: Horizontal(g6)
    c: Vertical(g5)
    c: Vertical(g7)
    c: Equal(g1,g5)
    c: Equal(g4,g2)
    c: Vertical(g1,g4)
    c: DistanceX(g0,g0) = 3
    c: DistanceY(g1,g1) = 5.8
    c: DistanceY(g5,g1) = 10
    c: DistanceY(g-1,g5) = 7.1
    c: DistanceX(g5,g-1) = 3
FEATURE [Sketcher::SketchObject] Sketch1904
  MapMode = 5
  Support = -> [XY_Plane575]
  sketch-geometry (1):
    g0: Circle CenterX=0 CenterY=0 CenterZ=0 NormalX=0 NormalY=0 NormalZ=1 AngleXU=0 Radius=2.75
  constraints (2):
    c: Coincident(g0,g-1)
    c: Radius(g0) = 2.75
FEATURE [PartDesign::Pad] Pad716  label="M3x8 Head092"
  Length = 3
  Length2 = 100
  Profile = -> Sketch1904
  Type = 0
FEATURE [Sketcher::SketchObject] Sketch1613
  MapMode = 5
  Placement = pos=(0,0,3) rot=(0,0,1;0rad)
  Support = -> [Pad716]
  sketch-geometry (1):
    g0: Circle CenterX=0 CenterY=0 CenterZ=0 NormalX=0 NormalY=0 NormalZ=1 AngleXU=0 Radius=1.5
  constraints (2):
    c: Coincident(g0,g-1)
    c: Radius(g0) = 1.5
FEATURE [PartDesign::Pad] Pad705  label="M3x8 Thread087"
  BaseFeature = -> Pad716
  Length = 8
  Length2 = 100
  Profile = -> Sketch1613
  Type = 0
FEATURE [Sketcher::SketchObject] Sketch1609
  MapMode = 5
  Placement = pos=(0,0,0) rot=(1,0,0;3.14159rad)
  Support = -> [Pad705]
  sketch-geometry (7):
    g0: LineSegment StartX=1.275 StartY=0.736122 StartZ=0 EndX=0 EndY=1.47224 EndZ=0
    g1: LineSegment StartX=0 StartY=1.47224 StartZ=0 EndX=-1.275 EndY=0.736122 EndZ=0
    g2: LineSegment StartX=-1.275 StartY=0.736122 StartZ=0 EndX=-1.275 EndY=-0.736122 EndZ=0
    g3: LineSegment StartX=-1.275 StartY=-0.736122 StartZ=0 EndX=1.34766e-11 EndY=-1.47224 EndZ=0
    g4: LineSegment StartX=1.34766e-11 StartY=-1.47224 StartZ=0 EndX=1.275 EndY=-0.736122 EndZ=0
    g5: LineSegment StartX=1.275 StartY=-0.736122 StartZ=0 EndX=1.275 EndY=0.736122 EndZ=0
    g6: Circle [constr] CenterX=0 CenterY=0 CenterZ=0 NormalX=0 NormalY=0 NormalZ=1 AngleXU=0 Radius=1.47224
  constraints (16):
    c: Coincident(g0,g1)
    c: Coincident(g1,g2)
    c: Coincident(g2,g3)
    c: Coincident(g3,g4)
    c: Coincident(g4,g5)
    c: Coincident(g5,g0)
    c: Equal(g0, g1-g5) x5
    c: PointOnObject(g0,g6)
    c: PointOnObject(g1,g6)
    c: PointOnObject(g2,g6)
    c: PointOnObject(g3,g6)
    c: PointOnObject(g4,g6)
    c: PointOnObject(g5,g6)
    c: Coincident(g6,g-1)
    c: PointOnObject(g0,g-2)
    c: DistanceX(g1,g0) = 2.55
FEATURE [PartDesign::Pocket] Pocket616  label="M3x8 Wrench091"
  BaseFeature = -> Pad705
  Length = 1.3
  Length2 = 100
  Profile = -> Sketch1609
  Type = 0
FEATURE [PartDesign::Chamfer] Chamfer372  label="M3x8 Smooth095"
  Base = -> Pocket616 [Face11,Edge2,Edge24,Edge3]
  BaseFeature = -> Pocket616
  Size = 0.2
FEATURE [PartDesign::Chamfer] Chamfer381  label="M3x8 Smooth098"
  Base = -> Pocket612 [Face11,Edge2,Edge24,Edge3]
  BaseFeature = -> Pocket612
  Size = 0.2
FEATURE [PartDesign::Pad] Pad789  label="M3 Nut Primitive155"
  Length = 1.2
  Length2 = 1.2
  Profile = -> Sketch1640
  Type = 4
FEATURE [Sketcher::SketchObject] Sketch1631
  ExternalGeometry = -> [Pad789]
  MapMode = 5
  Placement = pos=(0,0,0) rot=(0.57735,0.57735,0.57735;2.0944rad)
  Support = -> [YZ_Plane604]
  sketch-geometry (6):
    g0: LineSegment StartX=-2.67543 StartY=1.2 StartZ=0 EndX=-3.67543 EndY=1.2 EndZ=0
    g1: LineSegment StartX=-3.67543 StartY=1.2 StartZ=0 EndX=-3.67543 EndY=-1.2 EndZ=0
    g2: LineSegment StartX=-3.67543 StartY=-1.2 StartZ=0 EndX=-2.67543 EndY=-1.2 EndZ=0
    g3: LineSegment StartX=-2.67543 StartY=-1.2 StartZ=0 EndX=-3.17543 EndY=-1 EndZ=0
    g4: LineSegment StartX=-3.17543 StartY=-1 StartZ=0 EndX=-3.17543 EndY=1 EndZ=0
    g5: LineSegment StartX=-3.17543 StartY=1 StartZ=0 EndX=-2.67543 EndY=1.2 EndZ=0
  constraints (15):
    c: Horizontal(g0)
    c: Coincident(g0,g1)
    c: Coincident(g1,g2)
    c: Coincident(g2,g3)
    c: Coincident(g3,g4)
    c: Coincident(g4,g5)
    c: Coincident(g5,g0)
    c: Symmetric(g4,g3,g-1)
    c: Symmetric(g0,g2,g-1)
    c: Symmetric(g1,g0,g-1)
    c: DistanceX(g0,g4) = 0.5
    c: DistanceY(g3,g4) = 2
    c: DistanceY(g1,g0) = 2.4
    c: PointOnObject(g3,g-3)
    c: DistanceX(g4,g0) = 0.5
FEATURE [PartDesign::Pad] Pad790
  Length = 5
  Length2 = 100
  Profile = -> Sketch1825
  Type = 0
FEATURE [Sketcher::SketchObject] Sketch1745
  MapMode = 5
  Placement = pos=(0,0,0) rot=(1,0,0;3.14159rad)
  Support = -> [Pad790]
  sketch-geometry (1):
    g0: Circle CenterX=0 CenterY=0 CenterZ=0 NormalX=0 NormalY=0 NormalZ=1 AngleXU=0 Radius=2.5
  constraints (2):
    c: Coincident(g0,g-1)
    c: Radius(g0) = 2.5
FEATURE [PartDesign::Pad] Pad793  label="M3x8 Head098"
  Length = 2
  Length2 = 100
  Profile = -> Sketch1742
  Type = 0
FEATURE [Sketcher::SketchObject] Sketch1738
  MapMode = 5
  Placement = pos=(0,0,2) rot=(0,0,1;0rad)
  Support = -> [Pad793]
  sketch-geometry (1):
    g0: Circle CenterX=0 CenterY=0 CenterZ=0 NormalX=0 NormalY=0 NormalZ=1 AngleXU=0 Radius=1
  constraints (2):
    c: Coincident(g0,g-1)
    c: Radius(g0) = 1
FEATURE [PartDesign::Pad] Pad794  label="Baseblock017"
  Length = 26.6
  Length2 = 100
  Profile = -> Sketch1642
  Type = 0
FEATURE [Sketcher::SketchObject] Sketch1752
  MapMode = 5
  Placement = pos=(0,0,26.6) rot=(0,0,1;0rad)
  Support = -> [Pad794]
  sketch-geometry (4):
    g0: LineSegment StartX=-10 StartY=-26.8 StartZ=0 EndX=10 EndY=-26.8 EndZ=0
    g1: LineSegment StartX=10 StartY=-26.8 StartZ=0 EndX=10 EndY=26.8 EndZ=0
    g2: LineSegment StartX=10 StartY=26.8 StartZ=0 EndX=-10 EndY=26.8 EndZ=0
    g3: LineSegment StartX=-10 StartY=26.8 StartZ=0 EndX=-10 EndY=-26.8 EndZ=0
  constraints (10):
    c: Coincident(g0,g1)
    c: Coincident(g1,g2)
    c: Coincident(g2,g3)
    c: Coincident(g3,g0)
    c: Horizontal(g0)
    c: Vertical(g3)
    c: Symmetric(g1,g2,g-2)
    c: Symmetric(g1,g0,g-1)
    c: DistanceX(g2,g2) = 20
    c: DistanceY(g1,g1) = 53.6
FEATURE [PartDesign::Pad] Pad745
  BaseFeature = -> Pad794
  Length = 2.5
  Length2 = 100
  Profile = -> Sketch1752
  Type = 0
FEATURE [Sketcher::SketchObject] Sketch1623
  MapMode = 5
  Placement = pos=(0,0,29.1) rot=(0,0,1;0rad)
  Support = -> [Pad745]
  sketch-geometry (4):
    g0: LineSegment StartX=-10 StartY=-20.15 StartZ=0 EndX=10 EndY=-20.15 EndZ=0
    g1: LineSegment StartX=10 StartY=-20.15 StartZ=0 EndX=10 EndY=20.15 EndZ=0
    g2: LineSegment StartX=10 StartY=20.15 StartZ=0 EndX=-10 EndY=20.15 EndZ=0
    g3: LineSegment StartX=-10 StartY=20.15 StartZ=0 EndX=-10 EndY=-20.15 EndZ=0
  constraints (10):
    c: Coincident(g0,g1)
    c: Coincident(g1,g2)
    c: Coincident(g2,g3)
    c: Coincident(g3,g0)
    c: Horizontal(g0)
    c: Vertical(g3)
    c: Symmetric(g1,g2,g-2)
    c: Symmetric(g1,g0,g-1)
    c: DistanceX(g2,g2) = 20
    c: DistanceY(g1,g1) = 40.3
FEATURE [PartDesign::Pad] Pad792
  BaseFeature = -> Pad745
  Length = 6
  Length2 = 100
  Profile = -> Sketch1623
  Type = 0
FEATURE [Sketcher::SketchObject] Sketch1656
  ExternalGeometry = -> [Pad792]
  MapMode = 5
  Placement = pos=(0,0,35.1) rot=(0,0,1;0rad)
  Support = -> [Pad792]
  sketch-geometry (7):
    g0: ArcOfCircle CenterX=-3e-16 CenterY=10.15 CenterZ=0 NormalX=0 NormalY=0 NormalZ=1 AngleXU=0 Radius=9.5 StartAngle=5.9573 EndAngle=9.75066
    g1: LineSegment StartX=-9 StartY=7.10862 StartZ=0 EndX=-9 EndY=-14.15 EndZ=0
    g2: LineSegment StartX=-9 StartY=-14.15 StartZ=0 EndX=-5 EndY=-14.15 EndZ=0
    g3: LineSegment StartX=5 StartY=-14.15 StartZ=0 EndX=9 EndY=-14.15 EndZ=0
    g4: LineSegment StartX=9 StartY=-14.15 StartZ=0 EndX=9 EndY=7.10862 EndZ=0
    g5: ArcOfCircle CenterX=-3e-16 CenterY=-10.4 CenterZ=0 NormalX=0 NormalY=0 NormalZ=1 AngleXU=0 Radius=6.25 StartAngle=3.78509 EndAngle=5.63968
    g6: LineSegment [constr] StartX=0 StartY=-20.15 StartZ=0 EndX=0 EndY=-16.65 EndZ=0
  constraints (22):
    c: Symmetric(g0,g0,g-2)
    c: Coincident(g1,g0)
    c: Vertical(g1)
    c: Coincident(g2,g1)
    c: Horizontal(g2)
    c: Horizontal(g3)
    c: Coincident(g4,g3)
    c: Coincident(g4,g0)
    c: Vertical(g4)
    c: Symmetric(g2,g3,g-2)
    c: Coincident(g5,g2)
    c: Coincident(g5,g3)
    c: DistanceY(g-3,g3) = 6
    c: DistanceY(g0,g-4) = 10
    c: Radius(g0) = 9.5
    c: DistanceX(g0,g0) = 18
    c: PointOnObject(g6,g-3)
    c: PointOnObject(g6,g5)
    c: Vertical(g6)
    c: DistanceY(g6,g6) = 3.5
    c: DistanceX(g2,g3) = 10
    c: PointOnObject(g6,g-2)
FEATURE [PartDesign::Pad] Pad747
  BaseFeature = -> Pad792
  Length = 2.5
  Length2 = 100
  Profile = -> Sketch1656
  Type = 0
FEATURE [Sketcher::SketchObject] Sketch1620
  ExternalGeometry = -> [Pad747]
  MapMode = 5
  Placement = pos=(0,0,37.6) rot=(0,0,1;0rad)
  Support = -> [Pad747]
  sketch-geometry (1):
    g0: Circle CenterX=-3e-16 CenterY=10.15 CenterZ=0 NormalX=0 NormalY=0 NormalZ=1 AngleXU=0 Radius=6.5
  constraints (2):
    c: Coincident(g0,g-3)
    c: Radius(g0) = 6.5
FEATURE [PartDesign::Pad] Pad659
  BaseFeature = -> Pad747
  Length = 1
  Length2 = 100
  Profile = -> Sketch1620
  Type = 0
FEATURE [Sketcher::SketchObject] Sketch1630
  ExternalGeometry = -> [Pad659]
  MapMode = 5
  Placement = pos=(0,0,38.6) rot=(0,0,1;0rad)
  Support = -> [Pad659]
  sketch-geometry (1):
    g0: Circle CenterX=0 CenterY=10.15 CenterZ=0 NormalX=0 NormalY=0 NormalZ=1 AngleXU=0 Radius=5.5
  constraints (2):
    c: Coincident(g0,g-3)
    c: Radius(g0) = 5.5
FEATURE [PartDesign::Pad] Pad748
  BaseFeature = -> Pad659
  Length = 0.5
  Length2 = 100
  Profile = -> Sketch1630
  Type = 0
FEATURE [Sketcher::SketchObject] Sketch1635
  ExternalGeometry = -> [Pad748]
  MapMode = 5
  Placement = pos=(0,0,39.1) rot=(0,0,1;0rad)
  Support = -> [Pad748]
  sketch-geometry (1):
    g0: Circle CenterX=0 CenterY=10.15 CenterZ=0 NormalX=0 NormalY=0 NormalZ=1 AngleXU=0 Radius=3
  constraints (2):
    c: Coincident(g0,g-3)
    c: Radius(g0) = 3
FEATURE [PartDesign::Pad] Pad796
  Length = 10
  Length2 = 100
  Placement = pos=(0,0,0) rot=(1,0,0;1.5708rad)
  Profile = -> Sketch1636
  Reversed = true
  Type = 0
FEATURE [PartDesign::Groove] Groove164  label="M3 Nut Smooth156"
  Angle = 360
  Axis = (-2e-16,3e-16,1)
  Base = (0,0,0)
  BaseFeature = -> Pad754
  Profile = -> Sketch1616
  ReferenceAxis = -> Sketch1616 [V_Axis]
  Reversed = true
FEATURE [PartDesign::Chamfer] Chamfer303  label="M3 Nut Smooth Hole128"
  Base = -> Groove164 [Edge24,Edge23]
  BaseFeature = -> Groove164
  Size = 0.2
FEATURE [PartDesign::Pad] Pad797  label="M3 Nut Primitive156"
  Length = 0.6
  Length2 = 0.6
  Profile = -> Sketch1667
  Type = 4
FEATURE [Sketcher::SketchObject] Sketch1723
  ExternalGeometry = -> [Pad797]
  MapMode = 5
  Placement = pos=(0,0,0) rot=(0.57735,0.57735,0.57735;2.0944rad)
  Support = -> [YZ_Plane678]
  sketch-geometry (6):
    g0: LineSegment StartX=-1.9594 StartY=0.6 StartZ=0 EndX=-2.8094 EndY=0.6 EndZ=0
    g1: LineSegment StartX=-2.8094 StartY=0.6 StartZ=0 EndX=-2.8094 EndY=-0.6 EndZ=0
    g2: LineSegment StartX=-2.8094 StartY=-0.6 StartZ=0 EndX=-1.9594 EndY=-0.6 EndZ=0
    g3: LineSegment StartX=-1.9594 StartY=-0.6 StartZ=0 EndX=-2.3094 EndY=-0.4 EndZ=0
    g4: LineSegment StartX=-2.3094 StartY=-0.4 StartZ=0 EndX=-2.3094 EndY=0.4 EndZ=0
    g5: LineSegment StartX=-2.3094 StartY=0.4 StartZ=0 EndX=-1.9594 EndY=0.6 EndZ=0
  constraints (15):
    c: Horizontal(g0)
    c: Coincident(g0,g1)
    c: Coincident(g1,g2)
    c: Coincident(g2,g3)
    c: Coincident(g3,g4)
    c: Coincident(g4,g5)
    c: Coincident(g5,g0)
    c: Symmetric(g4,g3,g-1)
    c: Symmetric(g0,g2,g-1)
    c: Symmetric(g1,g0,g-1)
    c: DistanceX(g0,g4) = 0.5
    c: DistanceY(g3,g4) = 0.8
    c: DistanceY(g1,g0) = 1.2
    c: PointOnObject(g3,g-3)
    c: DistanceX(g4,g0) = 0.35
FEATURE [PartDesign::Groove] Groove165  label="M3 Nut Smooth157"
  Angle = 360
  Axis = (-2e-16,3e-16,1)
  Base = (0,0,0)
  BaseFeature = -> Pad789
  Profile = -> Sketch1631
  ReferenceAxis = -> Sketch1631 [V_Axis]
  Reversed = true
FEATURE [PartDesign::Chamfer] Chamfer348  label="M3 Nut Smooth Hole147"
  Base = -> Groove165 [Edge24,Edge23]
  BaseFeature = -> Groove165
  Size = 0.2
FEATURE [PartDesign::Pad] Pad798
  BaseFeature = -> Pad715
  Length = 2.5
  Length2 = 100
  Profile = -> Sketch1547
  Type = 0
FEATURE [Sketcher::SketchObject] Sketch1576
  MapMode = 5
  Placement = pos=(0,0,29.1) rot=(0,0,1;0rad)
  Support = -> [Pad798]
  sketch-geometry (4):
    g0: LineSegment StartX=-10 StartY=-20.15 StartZ=0 EndX=10 EndY=-20.15 EndZ=0
    g1: LineSegment StartX=10 StartY=-20.15 StartZ=0 EndX=10 EndY=20.15 EndZ=0
    g2: LineSegment StartX=10 StartY=20.15 StartZ=0 EndX=-10 EndY=20.15 EndZ=0
    g3: LineSegment StartX=-10 StartY=20.15 StartZ=0 EndX=-10 EndY=-20.15 EndZ=0
  constraints (10):
    c: Coincident(g0,g1)
    c: Coincident(g1,g2)
    c: Coincident(g2,g3)
    c: Coincident(g3,g0)
    c: Horizontal(g0)
    c: Vertical(g3)
    c: Symmetric(g1,g2,g-2)
    c: Symmetric(g1,g0,g-1)
    c: DistanceX(g2,g2) = 20
    c: DistanceY(g1,g1) = 40.3
FEATURE [PartDesign::Pad] Pad791
  BaseFeature = -> Pad798
  Length = 6
  Length2 = 100
  Profile = -> Sketch1576
  Type = 0
FEATURE [Sketcher::SketchObject] Sketch1571
  ExternalGeometry = -> [Pad791]
  MapMode = 5
  Placement = pos=(0,0,35.1) rot=(0,0,1;0rad)
  Support = -> [Pad791]
  sketch-geometry (7):
    g0: ArcOfCircle CenterX=-3e-16 CenterY=10.15 CenterZ=0 NormalX=0 NormalY=0 NormalZ=1 AngleXU=0 Radius=9.5 StartAngle=5.9573 EndAngle=9.75066
    g1: LineSegment StartX=-9 StartY=7.10862 StartZ=0 EndX=-9 EndY=-14.15 EndZ=0
    g2: LineSegment StartX=-9 StartY=-14.15 StartZ=0 EndX=-5 EndY=-14.15 EndZ=0
    g3: LineSegment StartX=5 StartY=-14.15 StartZ=0 EndX=9 EndY=-14.15 EndZ=0
    g4: LineSegment StartX=9 StartY=-14.15 StartZ=0 EndX=9 EndY=7.10862 EndZ=0
    g5: ArcOfCircle CenterX=-3e-16 CenterY=-10.4 CenterZ=0 NormalX=0 NormalY=0 NormalZ=1 AngleXU=0 Radius=6.25 StartAngle=3.78509 EndAngle=5.63968
    g6: LineSegment [constr] StartX=0 StartY=-20.15 StartZ=0 EndX=0 EndY=-16.65 EndZ=0
  constraints (22):
    c: Symmetric(g0,g0,g-2)
    c: Coincident(g1,g0)
    c: Vertical(g1)
    c: Coincident(g2,g1)
    c: Horizontal(g2)
    c: Horizontal(g3)
    c: Coincident(g4,g3)
    c: Coincident(g4,g0)
    c: Vertical(g4)
    c: Symmetric(g2,g3,g-2)
    c: Coincident(g5,g2)
    c: Coincident(g5,g3)
    c: DistanceY(g-3,g3) = 6
    c: DistanceY(g0,g-4) = 10
    c: Radius(g0) = 9.5
    c: DistanceX(g0,g0) = 18
    c: PointOnObject(g6,g-3)
    c: PointOnObject(g6,g5)
    c: Vertical(g6)
    c: DistanceY(g6,g6) = 3.5
    c: DistanceX(g2,g3) = 10
    c: PointOnObject(g6,g-2)
FEATURE [PartDesign::Pad] Pad799  label="M3 Nut Primitive157"
  Length = 1.2
  Length2 = 1.2
  Profile = -> Sketch1749
  Type = 4
FEATURE [Sketcher::SketchObject] Sketch1819
  ExternalGeometry = -> [Pad799]
  MapMode = 5
  Placement = pos=(0,0,0) rot=(0.57735,0.57735,0.57735;2.0944rad)
  Support = -> [YZ_Plane610]
  sketch-geometry (6):
    g0: LineSegment StartX=-2.67543 StartY=1.2 StartZ=0 EndX=-3.67543 EndY=1.2 EndZ=0
    g1: LineSegment StartX=-3.67543 StartY=1.2 StartZ=0 EndX=-3.67543 EndY=-1.2 EndZ=0
    g2: LineSegment StartX=-3.67543 StartY=-1.2 StartZ=0 EndX=-2.67543 EndY=-1.2 EndZ=0
    g3: LineSegment StartX=-2.67543 StartY=-1.2 StartZ=0 EndX=-3.17543 EndY=-1 EndZ=0
    g4: LineSegment StartX=-3.17543 StartY=-1 StartZ=0 EndX=-3.17543 EndY=1 EndZ=0
    g5: LineSegment StartX=-3.17543 StartY=1 StartZ=0 EndX=-2.67543 EndY=1.2 EndZ=0
  constraints (15):
    c: Horizontal(g0)
    c: Coincident(g0,g1)
    c: Coincident(g1,g2)
    c: Coincident(g2,g3)
    c: Coincident(g3,g4)
    c: Coincident(g4,g5)
    c: Coincident(g5,g0)
    c: Symmetric(g4,g3,g-1)
    c: Symmetric(g0,g2,g-1)
    c: Symmetric(g1,g0,g-1)
    c: DistanceX(g0,g4) = 0.5
    c: DistanceY(g3,g4) = 2
    c: DistanceY(g1,g0) = 2.4
    c: PointOnObject(g3,g-3)
    c: DistanceX(g4,g0) = 0.5
FEATURE [PartDesign::Groove] Groove151  label="M3 Nut Smooth143"
  Angle = 360
  Axis = (-2e-16,3e-16,1)
  Base = (0,0,0)
  BaseFeature = -> Pad799
  Profile = -> Sketch1819
  ReferenceAxis = -> Sketch1819 [V_Axis]
  Reversed = true
FEATURE [PartDesign::Chamfer] Chamfer326  label="M3 Nut Smooth Hole136"
  Base = -> Groove151 [Edge24,Edge23]
  BaseFeature = -> Groove151
  Size = 0.2
FEATURE [PartDesign::Pad] Pad800
  BaseFeature = -> Pad791
  Length = 2.5
  Length2 = 100
  Profile = -> Sketch1571
  Type = 0
FEATURE [Sketcher::SketchObject] Sketch1563
  ExternalGeometry = -> [Pad800]
  MapMode = 5
  Placement = pos=(0,0,37.6) rot=(0,0,1;0rad)
  Support = -> [Pad800]
  sketch-geometry (1):
    g0: Circle CenterX=-3e-16 CenterY=10.15 CenterZ=0 NormalX=0 NormalY=0 NormalZ=1 AngleXU=0 Radius=6.5
  constraints (2):
    c: Coincident(g0,g-3)
    c: Radius(g0) = 6.5
FEATURE [PartDesign::Pad] Pad721
  BaseFeature = -> Pad800
  Length = 1
  Length2 = 100
  Profile = -> Sketch1563
  Type = 0
FEATURE [Sketcher::SketchObject] Sketch1665
  ExternalGeometry = -> [Pad721]
  MapMode = 5
  Placement = pos=(0,0,38.6) rot=(0,0,1;0rad)
  Support = -> [Pad721]
  sketch-geometry (1):
    g0: Circle CenterX=0 CenterY=10.15 CenterZ=0 NormalX=0 NormalY=0 NormalZ=1 AngleXU=0 Radius=5.5
  constraints (2):
    c: Coincident(g0,g-3)
    c: Radius(g0) = 5.5
FEATURE [PartDesign::Pad] Pad801  label="M3 Nut Primitive158"
  Length = 1.2
  Length2 = 1.2
  Profile = -> Sketch1747
  Type = 4
FEATURE [Sketcher::SketchObject] Sketch1757
  ExternalGeometry = -> [Pad801]
  MapMode = 5
  Placement = pos=(0,0,0) rot=(0.57735,0.57735,0.57735;2.0944rad)
  Support = -> [YZ_Plane650]
  sketch-geometry (6):
    g0: LineSegment StartX=-2.67543 StartY=1.2 StartZ=0 EndX=-3.67543 EndY=1.2 EndZ=0
    g1: LineSegment StartX=-3.67543 StartY=1.2 StartZ=0 EndX=-3.67543 EndY=-1.2 EndZ=0
    g2: LineSegment StartX=-3.67543 StartY=-1.2 StartZ=0 EndX=-2.67543 EndY=-1.2 EndZ=0
    g3: LineSegment StartX=-2.67543 StartY=-1.2 StartZ=0 EndX=-3.17543 EndY=-1 EndZ=0
    g4: LineSegment StartX=-3.17543 StartY=-1 StartZ=0 EndX=-3.17543 EndY=1 EndZ=0
    g5: LineSegment StartX=-3.17543 StartY=1 StartZ=0 EndX=-2.67543 EndY=1.2 EndZ=0
  constraints (15):
    c: Horizontal(g0)
    c: Coincident(g0,g1)
    c: Coincident(g1,g2)
    c: Coincident(g2,g3)
    c: Coincident(g3,g4)
    c: Coincident(g4,g5)
    c: Coincident(g5,g0)
    c: Symmetric(g4,g3,g-1)
    c: Symmetric(g0,g2,g-1)
    c: Symmetric(g1,g0,g-1)
    c: DistanceX(g0,g4) = 0.5
    c: DistanceY(g3,g4) = 2
    c: DistanceY(g1,g0) = 2.4
    c: PointOnObject(g3,g-3)
    c: DistanceX(g4,g0) = 0.5
FEATURE [PartDesign::Groove] Groove152  label="M3 Nut Smooth144"
  Angle = 360
  Axis = (-2e-16,3e-16,1)
  Base = (0,0,0)
  BaseFeature = -> Pad801
  Profile = -> Sketch1757
  ReferenceAxis = -> Sketch1757 [V_Axis]
  Reversed = true
FEATURE [PartDesign::Chamfer] Chamfer371  label="M3 Nut Smooth Hole154"
  Base = -> Groove152 [Edge24,Edge23]
  BaseFeature = -> Groove152
  Size = 0.2
FEATURE [PartDesign::Pad] Pad802  label="M3 Nut Primitive159"
  Length = 1.2
  Length2 = 1.2
  Profile = -> Sketch1626
  Type = 4
FEATURE [Sketcher::SketchObject] Sketch1622
  ExternalGeometry = -> [Pad802]
  MapMode = 5
  Placement = pos=(0,0,0) rot=(0.57735,0.57735,0.57735;2.0944rad)
  Support = -> [YZ_Plane600]
  sketch-geometry (6):
    g0: LineSegment StartX=-2.67543 StartY=1.2 StartZ=0 EndX=-3.67543 EndY=1.2 EndZ=0
    g1: LineSegment StartX=-3.67543 StartY=1.2 StartZ=0 EndX=-3.67543 EndY=-1.2 EndZ=0
    g2: LineSegment StartX=-3.67543 StartY=-1.2 StartZ=0 EndX=-2.67543 EndY=-1.2 EndZ=0
    g3: LineSegment StartX=-2.67543 StartY=-1.2 StartZ=0 EndX=-3.17543 EndY=-1 EndZ=0
    g4: LineSegment StartX=-3.17543 StartY=-1 StartZ=0 EndX=-3.17543 EndY=1 EndZ=0
    g5: LineSegment StartX=-3.17543 StartY=1 StartZ=0 EndX=-2.67543 EndY=1.2 EndZ=0
  constraints (15):
    c: Horizontal(g0)
    c: Coincident(g0,g1)
    c: Coincident(g1,g2)
    c: Coincident(g2,g3)
    c: Coincident(g3,g4)
    c: Coincident(g4,g5)
    c: Coincident(g5,g0)
    c: Symmetric(g4,g3,g-1)
    c: Symmetric(g0,g2,g-1)
    c: Symmetric(g1,g0,g-1)
    c: DistanceX(g0,g4) = 0.5
    c: DistanceY(g3,g4) = 2
    c: DistanceY(g1,g0) = 2.4
    c: PointOnObject(g3,g-3)
    c: DistanceX(g4,g0) = 0.5
FEATURE [PartDesign::Groove] Groove134  label="M3 Nut Smooth128"
  Angle = 360
  Axis = (-2e-16,3e-16,1)
  Base = (0,0,0)
  BaseFeature = -> Pad802
  Profile = -> Sketch1622
  ReferenceAxis = -> Sketch1622 [V_Axis]
  Reversed = true
FEATURE [PartDesign::Chamfer] Chamfer373  label="M3 Nut Smooth Hole155"
  Base = -> Groove134 [Edge24,Edge23]
  BaseFeature = -> Groove134
  Size = 0.2
FEATURE [PartDesign::Pad] Pad803  label="M3x8 Head099"
  Length = 2
  Length2 = 100
  Profile = -> Sketch1663
  Type = 0
FEATURE [Sketcher::SketchObject] Sketch1737
  MapMode = 5
  Placement = pos=(0,0,2) rot=(0,0,1;0rad)
  Support = -> [Pad803]
  sketch-geometry (1):
    g0: Circle CenterX=0 CenterY=0 CenterZ=0 NormalX=0 NormalY=0 NormalZ=1 AngleXU=0 Radius=1
  constraints (2):
    c: Coincident(g0,g-1)
    c: Radius(g0) = 1
FEATURE [PartDesign::Pad] Pad804
  Length = 2
  Length2 = 100
  Profile = -> Sketch1715
  Type = 0
FEATURE [Sketcher::SketchObject] Sketch1714
  MapMode = 5
  Placement = pos=(0,0,2) rot=(0,0,1;0rad)
  Support = -> [Pad804]
  sketch-geometry (2):
    g0: Circle CenterX=0 CenterY=0 CenterZ=0 NormalX=0 NormalY=0 NormalZ=1 AngleXU=0 Radius=5
    g1: Circle CenterX=0 CenterY=0 CenterZ=0 NormalX=0 NormalY=0 NormalZ=1 AngleXU=0 Radius=3.5
  constraints (4):
    c: Coincident(g0,g-1)
    c: Coincident(g1,g0)
    c: Radius(g1) = 3.5
    c: Radius(g0) = 5
FEATURE [PartDesign::Pocket] Pocket672
  BaseFeature = -> Pad804
  Length = 1
  Length2 = 100
  Profile = -> Sketch1714
  Type = 0
FEATURE [Sketcher::SketchObject] Sketch1719
  MapMode = 5
  Placement = pos=(0,0,2) rot=(0,0,1;0rad)
  Support = -> [Pocket672]
  sketch-geometry (1):
    g0: Circle CenterX=0 CenterY=0 CenterZ=0 NormalX=0 NormalY=0 NormalZ=1 AngleXU=0 Radius=3
  constraints (2):
    c: Coincident(g0,g-1)
    c: Radius(g0) = 3
FEATURE [PartDesign::Pocket] Pocket671
  BaseFeature = -> Pocket672
  Length = 1
  Length2 = 100
  Profile = -> Sketch1719
  Type = 0
FEATURE [Sketcher::SketchObject] Sketch1725
  MapMode = 5
  Placement = pos=(0,0,1) rot=(0,0,1;0rad)
  Support = -> [Pocket671]
  sketch-geometry (1):
    g0: Circle CenterX=0 CenterY=0 CenterZ=0 NormalX=0 NormalY=0 NormalZ=1 AngleXU=0 Radius=1.5
  constraints (2):
    c: Coincident(g0,g-1)
    c: Radius(g0) = 1.5
FEATURE [PartDesign::Pocket] Pocket661
  BaseFeature = -> Pocket671
  Length = 5
  Length2 = 100
  Profile = -> Sketch1725
  Type = 0
FEATURE [Sketcher::SketchObject] Sketch1728
  MapMode = 5
  Placement = pos=(0,0,0) rot=(1,0,0;3.14159rad)
  Support = -> [Pocket661]
  sketch-geometry (2):
    g0: Circle CenterX=0 CenterY=0 CenterZ=0 NormalX=0 NormalY=0 NormalZ=1 AngleXU=0 Radius=4.5
    g1: Circle CenterX=0 CenterY=0 CenterZ=0 NormalX=0 NormalY=0 NormalZ=1 AngleXU=0 Radius=3
  constraints (4):
    c: Coincident(g0,g-1)
    c: Coincident(g1,g0)
    c: Radius(g0) = 4.5
    c: Radius(g1) = 3
FEATURE [PartDesign::Pad] Pad805  label="M3x8 Thread096"
  BaseFeature = -> Pad803
  Length = 8
  Length2 = 100
  Profile = -> Sketch1737
  Type = 0
FEATURE [Sketcher::SketchObject] Sketch1741
  MapMode = 5
  Placement = pos=(0,0,0) rot=(1,0,0;3.14159rad)
  Support = -> [Pad805]
  sketch-geometry (7):
    g0: LineSegment StartX=0.77 StartY=0.44456 StartZ=0 EndX=0 EndY=0.889119 EndZ=0
    g1: LineSegment StartX=0 StartY=0.889119 StartZ=0 EndX=-0.77 EndY=0.44456 EndZ=0
    g2: LineSegment StartX=-0.77 StartY=0.44456 StartZ=0 EndX=-0.77 EndY=-0.44456 EndZ=0
    g3: LineSegment StartX=-0.77 StartY=-0.44456 StartZ=0 EndX=3.85628e-11 EndY=-0.889119 EndZ=0
    g4: LineSegment StartX=3.85628e-11 StartY=-0.889119 StartZ=0 EndX=0.77 EndY=-0.44456 EndZ=0
    g5: LineSegment StartX=0.77 StartY=-0.44456 StartZ=0 EndX=0.77 EndY=0.44456 EndZ=0
    g6: Circle [constr] CenterX=0 CenterY=0 CenterZ=0 NormalX=0 NormalY=0 NormalZ=1 AngleXU=0 Radius=0.889119
  constraints (16):
    c: Coincident(g0,g1)
    c: Coincident(g1,g2)
    c: Coincident(g2,g3)
    c: Coincident(g3,g4)
    c: Coincident(g4,g5)
    c: Coincident(g5,g0)
    c: Equal(g0, g1-g5) x5
    c: PointOnObject(g0,g6)
    c: PointOnObject(g1,g6)
    c: PointOnObject(g2,g6)
    c: PointOnObject(g3,g6)
    c: PointOnObject(g4,g6)
    c: PointOnObject(g5,g6)
    c: Coincident(g6,g-1)
    c: PointOnObject(g0,g-2)
    c: DistanceX(g1,g0) = 1.54
FEATURE [PartDesign::Pocket] Pocket678  label="Nutholes003"
  BaseFeature = -> Pocket601
  Length = 56.5
  Length2 = 100
  Profile = -> Sketch1529
  Type = 0
FEATURE [Sketcher::SketchObject] Sketch1538
  MapMode = 5
  Placement = pos=(0,0,0) rot=(0,0.707107,0.707107;3.14159rad)
  Support = -> [Pocket678]
  sketch-geometry (4):
    g0: Circle CenterX=-52.5 CenterY=20 CenterZ=0 NormalX=0 NormalY=0 NormalZ=1 AngleXU=0 Radius=1.6
    g1: Circle CenterX=-52.5 CenterY=10 CenterZ=0 NormalX=0 NormalY=0 NormalZ=1 AngleXU=0 Radius=1.6
    g2: Circle CenterX=-4 CenterY=20 CenterZ=0 NormalX=0 NormalY=0 NormalZ=1 AngleXU=0 Radius=1.6
    g3: Circle CenterX=-4 CenterY=10 CenterZ=0 NormalX=0 NormalY=0 NormalZ=1 AngleXU=0 Radius=1.6
  constraints (12):
    c: Horizontal(g2,g0)
    c: Horizontal(g1,g3)
    c: Vertical(g3,g2)
    c: Vertical(g0,g1)
    c: Equal(g0,g1)
    c: Equal(g1,g2)
    c: Equal(g2,g3)
    c: Radius(g2) = 1.6
    c: DistanceX(g0,g2) = 48.5
    c: DistanceY(g3,g2) = 10
    c: DistanceY(g-1,g3) = 10
    c: DistanceX(g3,g-1) = 4
FEATURE [PartDesign::Pocket] Pocket618  label="Screwholes006"
  BaseFeature = -> Pocket678
  Length = 8.5
  Length2 = 100
  Profile = -> Sketch1538
  Type = 0
FEATURE [Sketcher::SketchObject] Sketch1621
  MapMode = 5
  Placement = pos=(56.5,0,0) rot=(0.57735,0.57735,0.57735;2.0944rad)
  Support = -> [Pocket618]
  sketch-geometry (4):
    g0: ArcOfCircle CenterX=-12 CenterY=11.5 CenterZ=0 NormalX=0 NormalY=0 NormalZ=1 AngleXU=0 Radius=2.5 StartAngle=3.14159 EndAngle=6.28319
    g1: LineSegment StartX=-14.5 StartY=11.5 StartZ=0 EndX=-14.5 EndY=25 EndZ=0
    g2: LineSegment StartX=-14.5 StartY=25 StartZ=0 EndX=-9.5 EndY=25 EndZ=0
    g3: LineSegment StartX=-9.5 StartY=25 StartZ=0 EndX=-9.5 EndY=11.5 EndZ=0
  constraints (13):
    c: Horizontal(g0,g0)
    c: Horizontal(g0,g0)
    c: Coincident(g1,g0)
    c: Vertical(g1)
    c: Coincident(g2,g1)
    c: Horizontal(g2)
    c: Coincident(g3,g2)
    c: Coincident(g3,g0)
    c: Vertical(g3)
    c: Radius(g0) = 2.5
    c: DistanceX(g0,g-1) = 12
    c: DistanceY(g-1,g0) = 11.5
    c: DistanceY(g-1,g2) = 25
FEATURE [PartDesign::Pocket] Pocket603  label="Servocable Pocket003"
  BaseFeature = -> Pocket618
  Length = 8
  Length2 = 100
  Profile = -> Sketch1621
  Type = 0
FEATURE [PartDesign::Fillet] Fillet195  label="Servocable Smooth Edges003"
  Base = -> Pocket603 [Edge48,Edge43]
  BaseFeature = -> Pocket603
  Radius = 0.5
FEATURE [Sketcher::SketchObject] Sketch1614
  MapMode = 5
  Placement = pos=(0,-22,0) rot=(1,0,0;1.5708rad)
  Support = -> [Fillet195]
  sketch-geometry (1):
    g0: Circle CenterX=38.25 CenterY=15 CenterZ=0 NormalX=0 NormalY=0 NormalZ=1 AngleXU=0 Radius=0.95
  constraints (3):
    c: DistanceY(g-1,g0) = 15
    c: DistanceX(g-1,g0) = 38.25
    c: Radius(g0) = 0.95
FEATURE [PartDesign::Pocket] Pocket609  label="Ball Bearing Pin Screwhole003"
  BaseFeature = -> Fillet195
  Length = 3
  Length2 = 100
  Profile = -> Sketch1614
  Type = 0
FEATURE [Sketcher::SketchObject] Sketch1903
  ExternalGeometry = -> [Pocket609]
  MapMode = 5
  Placement = pos=(0,-19,0) rot=(0,0.707107,0.707107;3.14159rad)
  Support = -> [Pocket609]
  sketch-geometry (7):
    g0: LineSegment StartX=-36.2 StartY=16.1836 StartZ=0 EndX=-38.25 EndY=17.3671 EndZ=0
    g1: LineSegment StartX=-38.25 StartY=17.3671 StartZ=0 EndX=-40.3 EndY=16.1836 EndZ=0
    g2: LineSegment StartX=-40.3 StartY=16.1836 StartZ=0 EndX=-40.3 EndY=13.8164 EndZ=0
    g3: LineSegment StartX=-40.3 StartY=13.8164 StartZ=0 EndX=-38.25 EndY=12.6329 EndZ=0
    g4: LineSegment StartX=-38.25 StartY=12.6329 StartZ=0 EndX=-36.2 EndY=13.8164 EndZ=0
    g5: LineSegment StartX=-36.2 StartY=13.8164 StartZ=0 EndX=-36.2 EndY=16.1836 EndZ=0
    g6: Circle [constr] CenterX=-38.25 CenterY=15 CenterZ=0 NormalX=0 NormalY=0 NormalZ=1 AngleXU=0 Radius=2.36714
  constraints (16):
    c: Coincident(g0,g1)
    c: Coincident(g1,g2)
    c: Coincident(g2,g3)
    c: Coincident(g3,g4)
    c: Coincident(g4,g5)
    c: Coincident(g5,g0)
    c: Equal(g0, g1-g5) x5
    c: PointOnObject(g0,g6)
    c: PointOnObject(g1,g6)
    c: PointOnObject(g2,g6)
    c: PointOnObject(g3,g6)
    c: PointOnObject(g4,g6)
    c: PointOnObject(g5,g6)
    c: Coincident(g6,g-3)
    c: Vertical(g5)
    c: DistanceX(g1,g0) = 4.1
FEATURE [PartDesign::Pocket] Pocket613  label="Ball Bearing Pin Nuthole003"
  BaseFeature = -> Pocket609
  Length = 1.5
  Length2 = 100
  Profile = -> Sketch1903
  Type = 0
FEATURE [PartDesign::Fillet] Fillet201  label="Smooth Counterpart Corner003"
  Base = -> Pocket613 [Edge3]
  BaseFeature = -> Pocket613
  Radius = 5
FEATURE [PartDesign::Fillet] Fillet196  label="Smooth Servo Pocket003"
  Base = -> Fillet201 [Edge80,Edge77,Edge76,Edge79,Edge95]
  BaseFeature = -> Fillet201
  Radius = 1
FEATURE [Sketcher::SketchObject] Sketch1527
  MapMode = 5
  Placement = pos=(0,0,0) rot=(0,0.707107,0.707107;3.14159rad)
  Support = -> [Fillet196]
  sketch-geometry (4):
    g0: LineSegment StartX=0 StartY=0 StartZ=0 EndX=-56.5 EndY=0 EndZ=0
    g1: LineSegment StartX=-56.5 StartY=0 StartZ=0 EndX=-56.5 EndY=5 EndZ=0
    g2: LineSegment StartX=-56.5 StartY=5 StartZ=0 EndX=0 EndY=5 EndZ=0
    g3: LineSegment StartX=0 StartY=5 StartZ=0 EndX=0 EndY=0 EndZ=0
  constraints (11):
    c: Coincident(g0,g1)
    c: Coincident(g1,g2)
    c: Coincident(g2,g3)
    c: Coincident(g3,g0)
    c: Horizontal(g0)
    c: Horizontal(g2)
    c: Vertical(g1)
    c: Vertical(g3)
    c: Coincident(g0,g-1)
    c: DistanceY(g1,g1) = 5
    c: DistanceX(g2,g2) = 56.5
FEATURE [PartDesign::Pad] Pad719  label="Elongate Baseplate003"
  BaseFeature = -> Fillet196
  Length = 10
  Length2 = 100
  Profile = -> Sketch1527
  Type = 0
FEATURE [PartDesign::Fillet] Fillet235  label="Smooth Edges019"
  Base = -> Pad719 [Edge135,Edge159]
  BaseFeature = -> Pad719
  Radius = 0.4
FEATURE [PartDesign::Pad] Pad806
  BaseFeature = -> Pad748
  Length = 4
  Length2 = 100
  Profile = -> Sketch1635
  Type = 0
FEATURE [Sketcher::SketchObject] Sketch1649
  ExternalGeometry = -> [Pad806]
  MapMode = 5
  Placement = pos=(0,0,43.1) rot=(0,0,1;0rad)
  Support = -> [Pad806]
  sketch-geometry (1):
    g0: Circle CenterX=0 CenterY=10.15 CenterZ=0 NormalX=0 NormalY=0 NormalZ=1 AngleXU=0 Radius=1.5
  constraints (2):
    c: Coincident(g0,g-3)
    c: Radius(g0) = 1.5
FEATURE [PartDesign::Pocket] Pocket574
  BaseFeature = -> Pad806
  Length = 5
  Length2 = 100
  Profile = -> Sketch1649
  Type = 0
FEATURE [Sketcher::SketchObject] Sketch1634
  MapMode = 5
  Placement = pos=(0,0,29.1) rot=(0,0,1;0rad)
  Support = -> [Pocket574]
  sketch-geometry (4):
    g0: Circle CenterX=-4.91157 CenterY=25.3 CenterZ=0 NormalX=0 NormalY=0 NormalZ=1 AngleXU=0 Radius=2.25
    g1: Circle CenterX=4.91157 CenterY=25.3 CenterZ=0 NormalX=0 NormalY=0 NormalZ=1 AngleXU=0 Radius=2.25
    g2: Circle CenterX=-4.91157 CenterY=-25.3 CenterZ=0 NormalX=0 NormalY=0 NormalZ=1 AngleXU=0 Radius=2.25
    g3: Circle CenterX=4.91157 CenterY=-25.3 CenterZ=0 NormalX=0 NormalY=0 NormalZ=1 AngleXU=0 Radius=2.25
  constraints (8):
    c: Equal(g3,g2)
    c: Equal(g2,g1)
    c: Equal(g1,g0)
    c: Radius(g1) = 2.25
    c: Symmetric(g1,g0,g-2)
    c: Symmetric(g3,g2,g-2)
    c: Symmetric(g3,g1,g-1)
    c: DistanceY(g3,g1) = 50.6
FEATURE [PartDesign::Pocket] Pocket628
  BaseFeature = -> Pocket574
  Length = 5
  Length2 = 100
  Profile = -> Sketch1634
  Type = 0
FEATURE [Sketcher::SketchObject] Sketch1627
  MapMode = 5
  Placement = pos=(0,0,29.1) rot=(0,0,1;0rad)
  Support = -> [Pocket628]
  sketch-geometry (8):
    g0: LineSegment StartX=-0.5 StartY=26.8 StartZ=0 EndX=0.5 EndY=26.8 EndZ=0
    g1: LineSegment StartX=0.5 StartY=26.8 StartZ=0 EndX=0.5 EndY=20.15 EndZ=0
    g2: LineSegment StartX=0.5 StartY=20.15 StartZ=0 EndX=-0.5 EndY=20.15 EndZ=0
    g3: LineSegment StartX=-0.5 StartY=20.15 StartZ=0 EndX=-0.5 EndY=26.8 EndZ=0
    g4: LineSegment StartX=-0.5 StartY=-20.15 StartZ=0 EndX=0.5 EndY=-20.15 EndZ=0
    g5: LineSegment StartX=0.5 StartY=-20.15 StartZ=0 EndX=0.5 EndY=-26.8 EndZ=0
    g6: LineSegment StartX=0.5 StartY=-26.8 StartZ=0 EndX=-0.5 EndY=-26.8 EndZ=0
    g7: LineSegment StartX=-0.5 StartY=-26.8 StartZ=0 EndX=-0.5 EndY=-20.15 EndZ=0
  constraints (20):
    c: Coincident(g0,g1)
    c: Coincident(g1,g2)
    c: Coincident(g2,g3)
    c: Coincident(g3,g0)
    c: Horizontal(g2)
    c: Vertical(g1)
    c: Vertical(g3)
    c: Coincident(g4,g5)
    c: Coincident(g5,g6)
    c: Coincident(g6,g7)
    c: Coincident(g7,g4)
    c: Horizontal(g6)
    c: Vertical(g7)
    c: Symmetric(g4,g4,g-2)
    c: Symmetric(g0,g0,g-2)
    c: Symmetric(g0,g5,g-1)
    c: DistanceY(g5,g0) = 53.6
    c: DistanceY(g4,g1) = 40.3
    c: DistanceX(g0,g0) = 1
    c: Symmetric(g4,g1,g-1)
FEATURE [PartDesign::Pad] Pad752
  BaseFeature = -> Pocket628
  Length = 2
  Length2 = 100
  Profile = -> Sketch1627
  Type = 0
FEATURE [Sketcher::SketchObject] Sketch1648
  ExternalGeometry = -> [Pad752]
  MapMode = 5
  Placement = pos=(0.5,0,0) rot=(0.57735,0.57735,0.57735;2.0944rad)
  Support = -> [Pad752]
  sketch-geometry (6):
    g0: LineSegment StartX=-26.8 StartY=29.1 StartZ=0 EndX=-26.8 EndY=31.1 EndZ=0
    g1: LineSegment StartX=-26.8 StartY=31.1 StartZ=0 EndX=-20.15 EndY=31.1 EndZ=0
    g2: LineSegment StartX=-20.15 StartY=31.1 StartZ=0 EndX=-26.8 EndY=29.1 EndZ=0
    g3: LineSegment StartX=20.15 StartY=31.1 StartZ=0 EndX=26.8 EndY=31.1 EndZ=0
    g4: LineSegment StartX=26.8 StartY=31.1 StartZ=0 EndX=26.8 EndY=29.1 EndZ=0
    g5: LineSegment StartX=26.8 StartY=29.1 StartZ=0 EndX=20.15 EndY=31.1 EndZ=0
  constraints (14):
    c: Vertical(g0)
    c: Coincident(g0,g1)
    c: Horizontal(g1)
    c: Coincident(g1,g2)
    c: Coincident(g2,g0)
    c: Coincident(g3,g4)
    c: Coincident(g4,g5)
    c: Coincident(g5,g3)
    c: Symmetric(g0,g4,g-2)
    c: Symmetric(g3,g0,g-2)
    c: Symmetric(g1,g3,g-2)
    c: DistanceX(g0,g3) = 53.6
    c: DistanceY(g4,g4) = 2
    c: Coincident(g3,g-3)
FEATURE [PartDesign::Pocket] Pocket575
  BaseFeature = -> Pad752
  Length = 1
  Length2 = 100
  Profile = -> Sketch1648
  Type = 0
FEATURE [PartDesign::Fillet] Fillet210
  Base = -> Pocket575 [Edge26,Edge27,Edge72,Edge63,Edge70,Edge78,Edge51,Edge49,Edge71,Edge50,Edge79,Edge86,Edge30,Edge21,Edge4,Edge29,Edge105,Edge107,Edge109,Edge111,Edge113,Edge114,Edge123]
  BaseFeature = -> Pocket575
  Radius = 0.4
FEATURE [Sketcher::SketchObject] Sketch1654
  MapMode = 5
  Placement = pos=(0,20.15,0) rot=(0,0.707107,0.707107;3.14159rad)
  Support = -> [Fillet210]
  sketch-geometry (4):
    g0: LineSegment StartX=-3.25 StartY=2 StartZ=0 EndX=3.25 EndY=2 EndZ=0
    g1: LineSegment StartX=3.25 StartY=2 StartZ=0 EndX=3.25 EndY=6 EndZ=0
    g2: LineSegment StartX=3.25 StartY=6 StartZ=0 EndX=-3.25 EndY=6 EndZ=0
    g3: LineSegment StartX=-3.25 StartY=6 StartZ=0 EndX=-3.25 EndY=2 EndZ=0
  constraints (11):
    c: Coincident(g0,g1)
    c: Coincident(g1,g2)
    c: Coincident(g2,g3)
    c: Coincident(g3,g0)
    c: Horizontal(g0)
    c: Vertical(g1)
    c: Vertical(g3)
    c: DistanceY(g-1,g0) = 2
    c: DistanceY(g1,g1) = 4
    c: Symmetric(g2,g1,g-2)
    c: DistanceX(g2,g2) = 6.5
FEATURE [PartDesign::Pad] Pad795
  BaseFeature = -> Fillet210
  Length = 1
  Length2 = 100
  Profile = -> Sketch1654
  Type = 0
FEATURE [Sketcher::SketchObject] Sketch1615
  MapMode = 5
  Placement = pos=(0,21.15,0) rot=(0,0.707107,0.707107;3.14159rad)
  Support = -> [Pad795]
  sketch-geometry (4):
    g0: LineSegment StartX=-2.75 StartY=5.5 StartZ=0 EndX=2.75 EndY=5.5 EndZ=0
    g1: LineSegment StartX=2.75 StartY=5.5 StartZ=0 EndX=2.75 EndY=2.5 EndZ=0
    g2: LineSegment StartX=2.75 StartY=2.5 StartZ=0 EndX=-2.75 EndY=2.5 EndZ=0
    g3: LineSegment StartX=-2.75 StartY=2.5 StartZ=0 EndX=-2.75 EndY=5.5 EndZ=0
  constraints (11):
    c: Coincident(g0,g1)
    c: Coincident(g1,g2)
    c: Coincident(g2,g3)
    c: Coincident(g3,g0)
    c: Horizontal(g0)
    c: Vertical(g1)
    c: Vertical(g3)
    c: Symmetric(g1,g2,g-2)
    c: DistanceY(g1,g0) = 3
    c: DistanceY(g-1,g1) = 2.5
    c: DistanceX(g0,g0) = 5.5
FEATURE [PartDesign::Pad] Pad652
  BaseFeature = -> Pad795
  Length = 4
  Length2 = 100
  Profile = -> Sketch1615
  Type = 0
FEATURE [Sketcher::SketchObject] Sketch1633
  MapMode = 5
  Placement = pos=(0,0,0) rot=(1,0,0;3.14159rad)
  Support = -> [Pad652]
  sketch-geometry (4):
    g0: LineSegment StartX=-10 StartY=-20.15 StartZ=0 EndX=10 EndY=-20.15 EndZ=0
    g1: LineSegment StartX=10 StartY=-20.15 StartZ=0 EndX=10 EndY=20.15 EndZ=0
    g2: LineSegment StartX=10 StartY=20.15 StartZ=0 EndX=-10 EndY=20.15 EndZ=0
    g3: LineSegment StartX=-10 StartY=20.15 StartZ=0 EndX=-10 EndY=-20.15 EndZ=0
  constraints (10):
    c: Coincident(g0,g1)
    c: Coincident(g1,g2)
    c: Coincident(g2,g3)
    c: Coincident(g3,g0)
    c: Horizontal(g0)
    c: Vertical(g1)
    c: Symmetric(g2,g1,g-2)
    c: Symmetric(g0,g2,g-1)
    c: DistanceX(g2,g2) = 20
    c: DistanceY(g1,g1) = 40.3
FEATURE [PartDesign::Pad] Pad755
  BaseFeature = -> Pad652
  Length = 2
  Length2 = 100
  Profile = -> Sketch1633
  Type = 0
FEATURE [PartDesign::Chamfer] Chamfer374
  Base = -> Pad755 [Face7]
  BaseFeature = -> Pad755
  Size = 1.5
FEATURE [PartDesign::Fillet] Fillet218
  Base = -> Chamfer374 [Edge1,Edge7,Edge18,Edge4,Face12]
  BaseFeature = -> Chamfer374
  Radius = 0.4
FEATURE [Sketcher::SketchObject] Sketch1641
  ExternalGeometry = -> [Fillet218]
  MapMode = 5
  Placement = pos=(0,0,43.1) rot=(0,0,1;0rad)
  Support = -> [Fillet218]
  sketch-geometry (1):
    g0: Circle CenterX=0 CenterY=10.15 CenterZ=0 NormalX=0 NormalY=0 NormalZ=1 AngleXU=0 Radius=3
  constraints (2):
    c: Coincident(g0,g-3)
    c: Radius(g0) = 3
FEATURE [PartDesign::Pocket] Pocket629
  BaseFeature = -> Fillet218
  Length = 5
  Length2 = 100
  Profile = -> Sketch1641
  Type = 0
FEATURE [PartDesign::Pad] Pad807  label="M3x8 Thread097"
  BaseFeature = -> Pad793
  Length = 8
  Length2 = 100
  Profile = -> Sketch1738
  Type = 0
FEATURE [Sketcher::SketchObject] Sketch1661
  MapMode = 5
  Placement = pos=(0,0,0) rot=(1,0,0;3.14159rad)
  Support = -> [Pad807]
  sketch-geometry (7):
    g0: LineSegment StartX=0.77 StartY=0.44456 StartZ=0 EndX=0 EndY=0.889119 EndZ=0
    g1: LineSegment StartX=0 StartY=0.889119 StartZ=0 EndX=-0.77 EndY=0.44456 EndZ=0
    g2: LineSegment StartX=-0.77 StartY=0.44456 StartZ=0 EndX=-0.77 EndY=-0.44456 EndZ=0
    g3: LineSegment StartX=-0.77 StartY=-0.44456 StartZ=0 EndX=3.85628e-11 EndY=-0.889119 EndZ=0
    g4: LineSegment StartX=3.85628e-11 StartY=-0.889119 StartZ=0 EndX=0.77 EndY=-0.44456 EndZ=0
    g5: LineSegment StartX=0.77 StartY=-0.44456 StartZ=0 EndX=0.77 EndY=0.44456 EndZ=0
    g6: Circle [constr] CenterX=0 CenterY=0 CenterZ=0 NormalX=0 NormalY=0 NormalZ=1 AngleXU=0 Radius=0.889119
  constraints (16):
    c: Coincident(g0,g1)
    c: Coincident(g1,g2)
    c: Coincident(g2,g3)
    c: Coincident(g3,g4)
    c: Coincident(g4,g5)
    c: Coincident(g5,g0)
    c: Equal(g0, g1-g5) x5
    c: PointOnObject(g0,g6)
    c: PointOnObject(g1,g6)
    c: PointOnObject(g2,g6)
    c: PointOnObject(g3,g6)
    c: PointOnObject(g4,g6)
    c: PointOnObject(g5,g6)
    c: Coincident(g6,g-1)
    c: PointOnObject(g0,g-2)
    c: DistanceX(g1,g0) = 1.54
FEATURE [PartDesign::Pad] Pad809  label="M3 Nut Primitive160"
  Length = 1.2
  Length2 = 1.2
  Profile = -> Sketch1637
  Type = 4
FEATURE [Sketcher::SketchObject] Sketch1628
  ExternalGeometry = -> [Pad809]
  MapMode = 5
  Placement = pos=(0,0,0) rot=(0.57735,0.57735,0.57735;2.0944rad)
  Support = -> [YZ_Plane605]
  sketch-geometry (6):
    g0: LineSegment StartX=-2.67543 StartY=1.2 StartZ=0 EndX=-3.67543 EndY=1.2 EndZ=0
    g1: LineSegment StartX=-3.67543 StartY=1.2 StartZ=0 EndX=-3.67543 EndY=-1.2 EndZ=0
    g2: LineSegment StartX=-3.67543 StartY=-1.2 StartZ=0 EndX=-2.67543 EndY=-1.2 EndZ=0
    g3: LineSegment StartX=-2.67543 StartY=-1.2 StartZ=0 EndX=-3.17543 EndY=-1 EndZ=0
    g4: LineSegment StartX=-3.17543 StartY=-1 StartZ=0 EndX=-3.17543 EndY=1 EndZ=0
    g5: LineSegment StartX=-3.17543 StartY=1 StartZ=0 EndX=-2.67543 EndY=1.2 EndZ=0
  constraints (15):
    c: Horizontal(g0)
    c: Coincident(g0,g1)
    c: Coincident(g1,g2)
    c: Coincident(g2,g3)
    c: Coincident(g3,g4)
    c: Coincident(g4,g5)
    c: Coincident(g5,g0)
    c: Symmetric(g4,g3,g-1)
    c: Symmetric(g0,g2,g-1)
    c: Symmetric(g1,g0,g-1)
    c: DistanceX(g0,g4) = 0.5
    c: DistanceY(g3,g4) = 2
    c: DistanceY(g1,g0) = 2.4
    c: PointOnObject(g3,g-3)
    c: DistanceX(g4,g0) = 0.5
FEATURE [PartDesign::Groove] Groove153  label="M3 Nut Smooth145"
  Angle = 360
  Axis = (-2e-16,3e-16,1)
  Base = (0,0,0)
  BaseFeature = -> Pad809
  Profile = -> Sketch1628
  ReferenceAxis = -> Sketch1628 [V_Axis]
  Reversed = true
FEATURE [PartDesign::Chamfer] Chamfer346  label="M3 Nut Smooth Hole145"
  Base = -> Groove153 [Edge24,Edge23]
  BaseFeature = -> Groove153
  Size = 0.2
FEATURE [PartDesign::Pad] Pad810  label="M3x8 Thread099"
  BaseFeature = -> Pad695
  Length = 8
  Length2 = 100
  Profile = -> Sketch1729
  Type = 0
FEATURE [Sketcher::SketchObject] Sketch1740
  MapMode = 5
  Placement = pos=(0,0,0) rot=(1,0,0;3.14159rad)
  Support = -> [Pad810]
  sketch-geometry (7):
    g0: LineSegment StartX=0.77 StartY=0.44456 StartZ=0 EndX=0 EndY=0.889119 EndZ=0
    g1: LineSegment StartX=0 StartY=0.889119 StartZ=0 EndX=-0.77 EndY=0.44456 EndZ=0
    g2: LineSegment StartX=-0.77 StartY=0.44456 StartZ=0 EndX=-0.77 EndY=-0.44456 EndZ=0
    g3: LineSegment StartX=-0.77 StartY=-0.44456 StartZ=0 EndX=3.85628e-11 EndY=-0.889119 EndZ=0
    g4: LineSegment StartX=3.85628e-11 StartY=-0.889119 StartZ=0 EndX=0.77 EndY=-0.44456 EndZ=0
    g5: LineSegment StartX=0.77 StartY=-0.44456 StartZ=0 EndX=0.77 EndY=0.44456 EndZ=0
    g6: Circle [constr] CenterX=0 CenterY=0 CenterZ=0 NormalX=0 NormalY=0 NormalZ=1 AngleXU=0 Radius=0.889119
  constraints (16):
    c: Coincident(g0,g1)
    c: Coincident(g1,g2)
    c: Coincident(g2,g3)
    c: Coincident(g3,g4)
    c: Coincident(g4,g5)
    c: Coincident(g5,g0)
    c: Equal(g0, g1-g5) x5
    c: PointOnObject(g0,g6)
    c: PointOnObject(g1,g6)
    c: PointOnObject(g2,g6)
    c: PointOnObject(g3,g6)
    c: PointOnObject(g4,g6)
    c: PointOnObject(g5,g6)
    c: Coincident(g6,g-1)
    c: PointOnObject(g0,g-2)
    c: DistanceX(g1,g0) = 1.54
FEATURE [PartDesign::Pad] Pad811  label="M3 Nut Primitive161"
  Length = 0.6
  Length2 = 0.6
  Profile = -> Sketch1660
  Type = 4
FEATURE [Sketcher::SketchObject] Sketch1688
  ExternalGeometry = -> [Pad811]
  MapMode = 5
  Placement = pos=(0,0,0) rot=(0.57735,0.57735,0.57735;2.0944rad)
  Support = -> [YZ_Plane647]
  sketch-geometry (6):
    g0: LineSegment StartX=-1.9594 StartY=0.6 StartZ=0 EndX=-2.8094 EndY=0.6 EndZ=0
    g1: LineSegment StartX=-2.8094 StartY=0.6 StartZ=0 EndX=-2.8094 EndY=-0.6 EndZ=0
    g2: LineSegment StartX=-2.8094 StartY=-0.6 StartZ=0 EndX=-1.9594 EndY=-0.6 EndZ=0
    g3: LineSegment StartX=-1.9594 StartY=-0.6 StartZ=0 EndX=-2.3094 EndY=-0.4 EndZ=0
    g4: LineSegment StartX=-2.3094 StartY=-0.4 StartZ=0 EndX=-2.3094 EndY=0.4 EndZ=0
    g5: LineSegment StartX=-2.3094 StartY=0.4 StartZ=0 EndX=-1.9594 EndY=0.6 EndZ=0
  constraints (15):
    c: Horizontal(g0)
    c: Coincident(g0,g1)
    c: Coincident(g1,g2)
    c: Coincident(g2,g3)
    c: Coincident(g3,g4)
    c: Coincident(g4,g5)
    c: Coincident(g5,g0)
    c: Symmetric(g4,g3,g-1)
    c: Symmetric(g0,g2,g-1)
    c: Symmetric(g1,g0,g-1)
    c: DistanceX(g0,g4) = 0.5
    c: DistanceY(g3,g4) = 0.8
    c: DistanceY(g1,g0) = 1.2
    c: PointOnObject(g3,g-3)
    c: DistanceX(g4,g0) = 0.35
FEATURE [PartDesign::Groove] Groove167  label="M3 Nut Smooth159"
  Angle = 360
  Axis = (-2e-16,3e-16,1)
  Base = (0,0,0)
  BaseFeature = -> Pad811
  Profile = -> Sketch1688
  ReferenceAxis = -> Sketch1688 [V_Axis]
  Reversed = true
FEATURE [PartDesign::Chamfer] Chamfer387  label="M3 Nut Smooth Hole162"
  Base = -> Groove167 [Edge24,Edge23]
  BaseFeature = -> Groove167
  Size = 0.2
FEATURE [PartDesign::Pocket] Pocket684  label="M3x8 Wrench098"
  BaseFeature = -> Pad805
  Length = 1
  Length2 = 100
  Profile = -> Sketch1741
  Type = 0
FEATURE [PartDesign::Chamfer] Chamfer321  label="M3x8 Smooth083"
  Base = -> Pocket684 [Face11,Edge2,Edge24,Edge3]
  BaseFeature = -> Pocket684
  Size = 0.2
FEATURE [PartDesign::Pad] Pad812  label="M3 Nut Primitive162"
  Length = 0.6
  Length2 = 0.6
  Profile = -> Sketch1662
  Type = 4
FEATURE [Sketcher::SketchObject] Sketch1726
  ExternalGeometry = -> [Pad812]
  MapMode = 5
  Placement = pos=(0,0,0) rot=(0.57735,0.57735,0.57735;2.0944rad)
  Support = -> [YZ_Plane668]
  sketch-geometry (6):
    g0: LineSegment StartX=-1.9594 StartY=0.6 StartZ=0 EndX=-2.8094 EndY=0.6 EndZ=0
    g1: LineSegment StartX=-2.8094 StartY=0.6 StartZ=0 EndX=-2.8094 EndY=-0.6 EndZ=0
    g2: LineSegment StartX=-2.8094 StartY=-0.6 StartZ=0 EndX=-1.9594 EndY=-0.6 EndZ=0
    g3: LineSegment StartX=-1.9594 StartY=-0.6 StartZ=0 EndX=-2.3094 EndY=-0.4 EndZ=0
    g4: LineSegment StartX=-2.3094 StartY=-0.4 StartZ=0 EndX=-2.3094 EndY=0.4 EndZ=0
    g5: LineSegment StartX=-2.3094 StartY=0.4 StartZ=0 EndX=-1.9594 EndY=0.6 EndZ=0
  constraints (15):
    c: Horizontal(g0)
    c: Coincident(g0,g1)
    c: Coincident(g1,g2)
    c: Coincident(g2,g3)
    c: Coincident(g3,g4)
    c: Coincident(g4,g5)
    c: Coincident(g5,g0)
    c: Symmetric(g4,g3,g-1)
    c: Symmetric(g0,g2,g-1)
    c: Symmetric(g1,g0,g-1)
    c: DistanceX(g0,g4) = 0.5
    c: DistanceY(g3,g4) = 0.8
    c: DistanceY(g1,g0) = 1.2
    c: PointOnObject(g3,g-3)
    c: DistanceX(g4,g0) = 0.35
FEATURE [PartDesign::Groove] Groove168  label="M3 Nut Smooth160"
  Angle = 360
  Axis = (-2e-16,3e-16,1)
  Base = (0,0,0)
  BaseFeature = -> Pad812
  Profile = -> Sketch1726
  ReferenceAxis = -> Sketch1726 [V_Axis]
  Reversed = true
FEATURE [PartDesign::Chamfer] Chamfer385  label="M3 Nut Smooth Hole161"
  Base = -> Groove168 [Edge24,Edge23]
  BaseFeature = -> Groove168
  Size = 0.2
FEATURE [PartDesign::Pad] Pad813  label="Baseplate033"
  Length = 5
  Length2 = 100
  Profile = -> Sketch1731
  Type = 0
FEATURE [Sketcher::SketchObject] Sketch1712
  MapMode = 5
  Placement = pos=(40,-9.6e-15,0) rot=(0.57735,0.57735,0.57735;2.0944rad)
  Support = -> [Pad813]
  sketch-geometry (4):
    g0: ArcOfCircle CenterX=35 CenterY=-21 CenterZ=0 NormalX=0 NormalY=0 NormalZ=1 AngleXU=0 Radius=26 StartAngle=1.17601 EndAngle=1.5708
    g1: LineSegment StartX=35 StartY=5 StartZ=0 EndX=35 EndY=6 EndZ=0
    g2: LineSegment StartX=35 StartY=6 StartZ=0 EndX=45 EndY=6 EndZ=0
    g3: LineSegment StartX=45 StartY=6 StartZ=0 EndX=45 EndY=3 EndZ=0
  constraints (13):
    c: Coincident(g1,g0)
    c: Vertical(g1)
    c: Horizontal(g2)
    c: Coincident(g3,g2)
    c: Vertical(g3)
    c: Coincident(g0,g3)
    c: Coincident(g1,g2)
    c: DistanceY(g1,g1) = 1
    c: DistanceY(g3,g3) = 3
    c: DistanceX(g2,g2) = 10
    c: DistanceY(g-1,g0) = 5
    c: DistanceX(g-1,g0) = 45
    c: Perpendicular(g0,g1)
FEATURE [PartDesign::SubtractivePipe] SubtractivePipe016  label="Smooth Surfaces007"
  AuxilleryCurvelinear = true
  AuxillerySpineTangent = false
  BaseFeature = -> Pad813
  Binormal = (0,0,0)
  Mode = 0
  Profile = -> Sketch1712
  Spine = -> Pad813 [Edge19,Edge22,Edge24,Edge4,Edge7,Edge10,Edge13]
  SpineTangent = false
  Transformation = 0
  Transition = 0
FEATURE [Sketcher::SketchObject] Sketch1734
  MapMode = 5
  Placement = pos=(0,0,5) rot=(0,0,1;0rad)
  Support = -> [SubtractivePipe016]
  sketch-geometry (3):
    g0: Circle [constr] CenterX=0 CenterY=15 CenterZ=0 NormalX=0 NormalY=0 NormalZ=1 AngleXU=0 Radius=35
    g1: Circle CenterX=28.7228 CenterY=35 CenterZ=0 NormalX=0 NormalY=0 NormalZ=1 AngleXU=0 Radius=2.85
    g2: Circle CenterX=33.541 CenterY=25 CenterZ=0 NormalX=0 NormalY=0 NormalZ=1 AngleXU=0 Radius=2.85
  constraints (9):
    c: PointOnObject(g1,g0)
    c: PointOnObject(g2,g0)
    c: Radius(g0) = 35
    c: Equal(g2,g1)
    c: Radius(g1) = 2.85
    c: DistanceY(g2,g1) = 10
    c: DistanceY(g-1,g0) = 15
    c: DistanceY(g0,g2) = 10
    c: DistanceX(g-1,g0) = 0
FEATURE [PartDesign::Fillet] Fillet239  label="Smooth Edges020"
  Base = -> SubtractivePipe016 [Edge21]
  BaseFeature = -> SubtractivePipe016
  Radius = 1.5
FEATURE [Sketcher::SketchObject] Sketch1721
  MapMode = 5
  Placement = pos=(0,0,5) rot=(0,0,1;0rad)
  Support = -> [Fillet239]
  sketch-geometry (33):
    g0: LineSegment [constr] StartX=11.6913 StartY=6.75 StartZ=0 EndX=0 EndY=13.5 EndZ=0
    g1: LineSegment [constr] StartX=0 StartY=13.5 StartZ=0 EndX=-11.6913 EndY=6.75 EndZ=0
    g2: LineSegment [constr] StartX=-11.6913 StartY=6.75 StartZ=0 EndX=-11.6913 EndY=-6.75 EndZ=0
    g3: LineSegment [constr] StartX=-11.6913 StartY=-6.75 StartZ=0 EndX=0 EndY=-13.5 EndZ=0
    g4: LineSegment [constr] StartX=-6e-16 StartY=-13.5 StartZ=0 EndX=11.6913 EndY=-6.75 EndZ=0
    g5: LineSegment [constr] StartX=11.6913 StartY=-6.75 StartZ=0 EndX=11.6913 EndY=6.75 EndZ=0
    g6: Circle [constr] CenterX=0 CenterY=0 CenterZ=0 NormalX=0 NormalY=0 NormalZ=1 AngleXU=0 Radius=13.5
    g7: LineSegment [constr] StartX=7.5 StartY=9e-16 StartZ=0 EndX=3.75 EndY=6.49519 EndZ=0
    g8: LineSegment [constr] StartX=3.75 StartY=6.49519 StartZ=0 EndX=-3.75 EndY=6.49519 EndZ=0
    g9: LineSegment [constr] StartX=-3.75 StartY=6.49519 StartZ=0 EndX=-7.5 EndY=-9e-16 EndZ=0
    g10: LineSegment [constr] StartX=-7.5 StartY=-9e-16 StartZ=0 EndX=-3.75 EndY=-6.49519 EndZ=0
    g11: LineSegment [constr] StartX=-3.75 StartY=-6.49519 StartZ=0 EndX=3.75 EndY=-6.49519 EndZ=0
    g12: LineSegment [constr] StartX=3.75 StartY=-6.49519 StartZ=0 EndX=7.5 EndY=9e-16 EndZ=0
    g13: Circle [constr] CenterX=0 CenterY=0 CenterZ=0 NormalX=0 NormalY=0 NormalZ=1 AngleXU=0 Radius=7.5
    g14: ArcOfCircle CenterX=11.6913 CenterY=-6.75 CenterZ=0 NormalX=0 NormalY=0 NormalZ=1 AngleXU=0 Radius=2.6 StartAngle=4.34694 EndAngle=7.17223
    g15: ArcOfCircle CenterX=-6e-16 CenterY=-13.5 CenterZ=0 NormalX=0 NormalY=0 NormalZ=1 AngleXU=0 Radius=2.6 StartAngle=3.29974 EndAngle=6.12503
    g16: ArcOfCircle CenterX=-11.6913 CenterY=-6.75 CenterZ=0 NormalX=0 NormalY=0 NormalZ=1 AngleXU=0 Radius=2.6 StartAngle=2.25255 EndAngle=5.07784
    g17: ArcOfCircle CenterX=-11.6913 CenterY=6.75 CenterZ=0 NormalX=0 NormalY=0 NormalZ=1 AngleXU=0 Radius=2.6 StartAngle=1.20535 EndAngle=4.03064
    g18: ArcOfCircle CenterX=0 CenterY=13.5 CenterZ=0 NormalX=0 NormalY=0 NormalZ=1 AngleXU=0 Radius=2.6 StartAngle=0.15815 EndAngle=2.98344
    g19: ArcOfCircle CenterX=11.6913 CenterY=6.75 CenterZ=0 NormalX=0 NormalY=0 NormalZ=1 AngleXU=0 Radius=2.6 StartAngle=5.39414 EndAngle=8.21943
    g20: LineSegment StartX=13.3297 StartY=4.73117 StartZ=0 EndX=7.5 EndY=9e-16 EndZ=0
    g21: LineSegment StartX=7.5 StartY=9e-16 StartZ=0 EndX=13.3297 EndY=-4.73117 EndZ=0
    g22: LineSegment StartX=10.7622 StartY=-9.17831 StartZ=0 EndX=3.75 EndY=-6.49519 EndZ=0
    g23: LineSegment StartX=3.75 StartY=-6.49519 StartZ=0 EndX=2.56755 EndY=-13.9095 EndZ=0
    g24: LineSegment StartX=-2.56755 StartY=-13.9095 StartZ=0 EndX=-3.75 EndY=-6.49519 EndZ=0
    g25: LineSegment StartX=-3.75 StartY=-6.49519 StartZ=0 EndX=-10.7622 EndY=-9.17831 EndZ=0
    g26: LineSegment StartX=-13.3297 StartY=-4.73117 StartZ=0 EndX=-7.5 EndY=-9e-16 EndZ=0
    g27: LineSegment StartX=-7.5 StartY=-9e-16 StartZ=0 EndX=-13.3297 EndY=4.73117 EndZ=0
    g28: LineSegment StartX=-10.7622 StartY=9.17831 StartZ=0 EndX=-3.75 EndY=6.49519 EndZ=0
    g29: LineSegment StartX=-3.75 StartY=6.49519 StartZ=0 EndX=-2.56755 EndY=13.9095 EndZ=0
    g30: LineSegment StartX=2.56755 StartY=13.9095 StartZ=0 EndX=3.75 EndY=6.49519 EndZ=0
    g31: LineSegment StartX=3.75 StartY=6.49519 StartZ=0 EndX=10.7622 EndY=9.17831 EndZ=0
    g32: LineSegment [constr] StartX=11.6913 StartY=6.75 StartZ=0 EndX=-11.6913 EndY=-6.75 EndZ=0
  constraints (70):
    c: Coincident(g0,g1)
    c: Coincident(g1,g2)
    c: Coincident(g2,g3)
    c: Coincident(g3,g4)
    c: Coincident(g4,g5)
    c: Coincident(g5,g0)
    c: Equal(g0, g1-g5) x5
    c: PointOnObject(g0,g6)
    c: PointOnObject(g1,g6)
    c: PointOnObject(g2,g6)
    c: PointOnObject(g3,g6)
    c: PointOnObject(g4,g6)
    c: PointOnObject(g5,g6)
    c: Coincident(g6,g-1)
    c: Radius(g6) = 13.5
    c: Coincident(g7,g8)
    c: Coincident(g8,g9)
    c: Coincident(g9,g10)
    c: Coincident(g10,g11)
    c: Coincident(g11,g12)
    c: Coincident(g12,g7)
    c: Equal(g7, g8-g12) x5
    c: PointOnObject(g7,g13)
    c: PointOnObject(g8,g13)
    c: PointOnObject(g9,g13)
    c: PointOnObject(g10,g13)
    c: PointOnObject(g11,g13)
    c: PointOnObject(g12,g13)
    c: Coincident(g13,g-1)
    c: Radius(g13) = 7.5
    c: Coincident(g14,g4)
    c: Coincident(g15,g3)
    c: Coincident(g16,g2)
    c: Coincident(g17,g1)
    c: Coincident(g18,g0)
    c: Coincident(g19,g0)
    c: Coincident(g20,g7)
    c: Coincident(g21,g20)
    c: Coincident(g22,g11)
    c: Coincident(g23,g22)
    c: Coincident(g24,g10)
    c: Coincident(g25,g24)
    c: Coincident(g26,g9)
    c: Coincident(g28,g8)
    c: Coincident(g29,g28)
    c: Coincident(g30,g7)
    c: Coincident(g31,g30)
    c: Tangent(g22,g14) = 1.5708
    c: Tangent(g23,g15) = 1.5708
    c: Tangent(g24,g15) = 1.5708
    c: Tangent(g26,g16) = 1.5708
    c: Tangent(g21,g14) = 1.5708
    c: Tangent(g16,g25) = 1.5708
    c: Tangent(g29,g18) = 1.5708
    c: Tangent(g30,g18) = 1.5708
    c: Tangent(g31,g19) = 1.5708
    c: Tangent(g20,g19) = 1.5708
    c: Tangent(g27,g17) = 1.5708
    c: Tangent(g17,g28) = 1.5708
    c: Coincident(g27,g26)
    c: Equal(g14,g15)
    c: Equal(g15,g16)
    c: Equal(g16,g17)
    c: Equal(g17,g18)
    c: Equal(g18,g19)
    c: Radius(g14) = 2.6
    c: Coincident(g32,g19)
    c: Coincident(g32,g16)
    c: Perpendicular(g32,g7)
    c: PointOnObject(g18,g-2)
FEATURE [PartDesign::Pocket] Pocket681  label="Screwheads Montage008"
  BaseFeature = -> Fillet239
  Length = 3
  Length2 = 100
  Profile = -> Sketch1734
  Type = 0
FEATURE [Sketcher::SketchObject] Sketch1720
  MapMode = 5
  Placement = pos=(0,0,2) rot=(0,0,1;0rad)
  Support = -> [Pocket681]
  sketch-geometry (3):
    g0: Circle [constr] CenterX=0 CenterY=15 CenterZ=0 NormalX=0 NormalY=0 NormalZ=1 AngleXU=0 Radius=35
    g1: Circle CenterX=28.7228 CenterY=35 CenterZ=0 NormalX=0 NormalY=0 NormalZ=1 AngleXU=0 Radius=1.6
    g2: Circle CenterX=33.541 CenterY=25 CenterZ=0 NormalX=0 NormalY=0 NormalZ=1 AngleXU=0 Radius=1.6
  constraints (9):
    c: Radius(g0) = 35
    c: PointOnObject(g1,g0)
    c: PointOnObject(g2,g0)
    c: Equal(g2,g1)
    c: Radius(g2) = 1.6
    c: DistanceY(g2,g1) = 10
    c: DistanceY(g-1,g0) = 15
    c: DistanceY(g0,g2) = 10
    c: DistanceX(g-1,g0) = 0
FEATURE [PartDesign::Groove] Groove169  label="M3 Nut Smooth161"
  Angle = 360
  Axis = (-2e-16,3e-16,1)
  Base = (0,0,0)
  BaseFeature = -> Pad686
  Profile = -> Sketch1717
  ReferenceAxis = -> Sketch1717 [V_Axis]
  Reversed = true
FEATURE [PartDesign::Chamfer] Chamfer363  label="M3 Nut Smooth Hole152"
  Base = -> Groove169 [Edge24,Edge23]
  BaseFeature = -> Groove169
  Size = 0.2
FEATURE [PartDesign::Pocket] Pocket685  label="Screwholes Montage008"
  BaseFeature = -> Pocket681
  Length = 3
  Length2 = 100
  Profile = -> Sketch1720
  Type = 0
FEATURE [PartDesign::Pocket] Pocket680  label="Servohorn015"
  BaseFeature = -> Pocket685
  Length = 2
  Length2 = 100
  Profile = -> Sketch1721
  Type = 0
FEATURE [PartDesign::Fillet] Fillet226  label="Smooth Servhohorn Edges004"
  Base = -> Pocket680 [Edge124,Edge122,Edge129,Edge121,Edge136,Edge120]
  BaseFeature = -> Pocket680
  Radius = 1
FEATURE [Sketcher::SketchObject] Sketch1727
  MapMode = 5
  Placement = pos=(0,0,3) rot=(0,0,1;0rad)
  Support = -> [Fillet226]
  sketch-geometry (14):
    g0: LineSegment [constr] StartX=0 StartY=10.5 StartZ=0 EndX=-9.09327 EndY=5.25 EndZ=0
    g1: LineSegment [constr] StartX=-9.09327 StartY=5.25 StartZ=0 EndX=-9.09327 EndY=-5.25 EndZ=0
    g2: LineSegment [constr] StartX=-9.09327 StartY=-5.25 StartZ=0 EndX=0 EndY=-10.5 EndZ=0
    g3: LineSegment [constr] StartX=0 StartY=-10.5 StartZ=0 EndX=9.09327 EndY=-5.25 EndZ=0
    g4: LineSegment [constr] StartX=9.09327 StartY=-5.25 StartZ=0 EndX=9.09327 EndY=5.25 EndZ=0
    g5: LineSegment [constr] StartX=9.09327 StartY=5.25 StartZ=0 EndX=0 EndY=10.5 EndZ=0
    g6: Circle [constr] CenterX=0 CenterY=0 CenterZ=0 NormalX=0 NormalY=0 NormalZ=1 AngleXU=0 Radius=10.5
    g7: LineSegment [constr] StartX=0 StartY=10.5 StartZ=0 EndX=0 EndY=-10.5 EndZ=0
    g8: Circle CenterX=0 CenterY=10.5 CenterZ=0 NormalX=0 NormalY=0 NormalZ=1 AngleXU=0 Radius=0.95
    g9: Circle CenterX=9.09327 CenterY=5.25 CenterZ=0 NormalX=0 NormalY=0 NormalZ=1 AngleXU=0 Radius=0.95
    g10: Circle CenterX=9.09327 CenterY=-5.25 CenterZ=0 NormalX=0 NormalY=0 NormalZ=1 AngleXU=0 Radius=0.95
    g11: Circle CenterX=0 CenterY=-10.5 CenterZ=0 NormalX=0 NormalY=0 NormalZ=1 AngleXU=0 Radius=0.95
    g12: Circle CenterX=-9.09327 CenterY=-5.25 CenterZ=0 NormalX=0 NormalY=0 NormalZ=1 AngleXU=0 Radius=0.95
    g13: Circle CenterX=-9.09327 CenterY=5.25 CenterZ=0 NormalX=0 NormalY=0 NormalZ=1 AngleXU=0 Radius=0.95
  constraints (30):
    c: Coincident(g0,g1)
    c: Coincident(g1,g2)
    c: Coincident(g2,g3)
    c: Coincident(g3,g4)
    c: Coincident(g4,g5)
    c: Coincident(g5,g0)
    c: Equal(g0, g1-g5) x5
    c: PointOnObject(g0,g6)
    c: PointOnObject(g1,g6)
    c: PointOnObject(g2,g6)
    c: PointOnObject(g3,g6)
    c: PointOnObject(g4,g6)
    c: PointOnObject(g5,g6)
    c: Coincident(g6,g-1)
    c: Coincident(g7,g0)
    c: Coincident(g7,g2)
    c: Radius(g6) = 10.5
    c: Coincident(g8,g0)
    c: Coincident(g9,g4)
    c: Coincident(g10,g3)
    c: Coincident(g11,g2)
    c: Coincident(g12,g1)
    c: Coincident(g13,g0)
    c: Equal(g13,g12)
    c: Equal(g12,g11)
    c: Equal(g11,g10)
    c: Equal(g10,g9)
    c: Equal(g9,g8)
    c: Radius(g8) = 0.95
    c: PointOnObject(g8,g-2)
FEATURE [PartDesign::Pocket] Pocket673  label="Servohorn Mounting Holes004"
  BaseFeature = -> Fillet226
  Length = 3
  Length2 = 100
  Profile = -> Sketch1727
  Type = 0
FEATURE [Sketcher::SketchObject] Sketch1711
  MapMode = 5
  Placement = pos=(0,0,3) rot=(0,0,1;0rad)
  Support = -> [Pocket673]
  sketch-geometry (1):
    g0: Circle CenterX=0 CenterY=0 CenterZ=0 NormalX=0 NormalY=0 NormalZ=1 AngleXU=0 Radius=6.15
  constraints (2):
    c: Coincident(g0,g-1)
    c: Radius(g0) = 6.15
FEATURE [PartDesign::Pocket] Pocket679  label="Servohorn Axis004"
  BaseFeature = -> Pocket673
  Length = 3
  Length2 = 100
  Profile = -> Sketch1711
  Type = 0
FEATURE [PartDesign::Fillet] Fillet228  label="Smooth End Egde004"
  Base = -> Pocket679 [Edge150]
  BaseFeature = -> Pocket679
  Radius = 0.4
FEATURE [PartDesign::Pocket] Pocket686  label="M3x8 Wrench099"
  BaseFeature = -> Pad807
  Length = 1
  Length2 = 100
  Profile = -> Sketch1661
  Type = 0
FEATURE [PartDesign::Chamfer] Chamfer319  label="M3x8 Smooth082"
  Base = -> Pocket686 [Face11,Edge2,Edge24,Edge3]
  BaseFeature = -> Pocket686
  Size = 0.2
FEATURE [PartDesign::Groove] Groove170  label="M3 Nut Smooth162"
  Angle = 360
  Axis = (-2e-16,3e-16,1)
  Base = (0,0,0)
  BaseFeature = -> Pad797
  Profile = -> Sketch1723
  ReferenceAxis = -> Sketch1723 [V_Axis]
  Reversed = true
FEATURE [PartDesign::Chamfer] Chamfer388  label="M3 Nut Smooth Hole163"
  Base = -> Groove170 [Edge24,Edge23]
  BaseFeature = -> Groove170
  Size = 0.2
FEATURE [PartDesign::Pocket] Pocket687  label="M3x8 Wrench100"
  BaseFeature = -> Pad810
  Length = 1
  Length2 = 100
  Profile = -> Sketch1740
  Type = 0
FEATURE [PartDesign::Chamfer] Chamfer384  label="M3x8 Smooth099"
  Base = -> Pocket687 [Face11,Edge2,Edge24,Edge3]
  BaseFeature = -> Pocket687
  Size = 0.2
FEATURE [PartDesign::Pad] Pad814  label="Baseplate034"
  Length = 5
  Length2 = 100
  Profile = -> Sketch1556
  Type = 0
FEATURE [Sketcher::SketchObject] Sketch1553
  MapMode = 5
  Placement = pos=(-40,0,0) rot=(0.57735,-0.57735,-0.57735;2.0944rad)
  Support = -> [Pad814]
  sketch-geometry (4):
    g0: ArcOfCircle CenterX=-25 CenterY=-21 CenterZ=0 NormalX=0 NormalY=0 NormalZ=1 AngleXU=0 Radius=26 StartAngle=1.17601 EndAngle=1.5708
    g1: LineSegment StartX=-25 StartY=5 StartZ=0 EndX=-25 EndY=6 EndZ=0
    g2: LineSegment StartX=-25 StartY=6 StartZ=0 EndX=-15 EndY=6 EndZ=0
    g3: LineSegment StartX=-15 StartY=6 StartZ=0 EndX=-15 EndY=3 EndZ=0
  constraints (13):
    c: Coincident(g1,g0)
    c: Vertical(g1)
    c: Horizontal(g2)
    c: Coincident(g3,g2)
    c: Vertical(g3)
    c: Coincident(g0,g3)
    c: Coincident(g1,g2)
    c: DistanceY(g1,g1) = 1
    c: DistanceY(g3,g3) = 3
    c: DistanceX(g2,g2) = 10
    c: DistanceY(g-1,g0) = 5
    c: Perpendicular(g0,g1)
    c: DistanceX(g0,g-1) = 15
FEATURE [PartDesign::SubtractivePipe] SubtractivePipe020  label="Smooth Surfaces008"
  AuxilleryCurvelinear = true
  AuxillerySpineTangent = false
  BaseFeature = -> Pad814
  Binormal = (0,0,0)
  Mode = 0
  Profile = -> Sketch1553
  Spine = -> Pad814 [Edge19,Edge22,Edge24,Edge4,Edge7,Edge10,Edge13]
  SpineTangent = false
  Transformation = 0
  Transition = 0
FEATURE [Sketcher::SketchObject] Sketch1684
  MapMode = 5
  Placement = pos=(0,0,5) rot=(0,0,1;0rad)
  Support = -> [SubtractivePipe020]
  sketch-geometry (3):
    g0: Circle [constr] CenterX=0 CenterY=15 CenterZ=0 NormalX=0 NormalY=0 NormalZ=1 AngleXU=0 Radius=35
    g1: Circle CenterX=-33.541 CenterY=25 CenterZ=0 NormalX=0 NormalY=0 NormalZ=1 AngleXU=0 Radius=2.85
    g2: Circle CenterX=-28.7228 CenterY=35 CenterZ=0 NormalX=0 NormalY=0 NormalZ=1 AngleXU=0 Radius=2.85
  constraints (9):
    c: PointOnObject(g1,g0)
    c: PointOnObject(g2,g0)
    c: Radius(g0) = 35
    c: Equal(g2,g1)
    c: Radius(g1) = 2.85
    c: DistanceY(g1,g2) = 10
    c: DistanceY(g-1,g0) = 15
    c: DistanceY(g0,g1) = 10
    c: DistanceX(g0,g-1) = 0
FEATURE [PartDesign::Fillet] Fillet194  label="Smooth Edges016"
  Base = -> SubtractivePipe020 [Edge21]
  BaseFeature = -> SubtractivePipe020
  Radius = 1.5
FEATURE [PartDesign::Pocket] Pocket604  label="Screwheads Montage007"
  BaseFeature = -> Fillet194
  Length = 3
  Length2 = 100
  Profile = -> Sketch1684
  Type = 0
FEATURE [Sketcher::SketchObject] Sketch1542
  MapMode = 5
  Placement = pos=(0,0,2) rot=(0,0,1;0rad)
  Support = -> [Pocket604]
  sketch-geometry (3):
    g0: Circle [constr] CenterX=0 CenterY=15 CenterZ=0 NormalX=0 NormalY=0 NormalZ=1 AngleXU=0 Radius=35
    g1: Circle CenterX=-33.541 CenterY=25 CenterZ=0 NormalX=0 NormalY=0 NormalZ=1 AngleXU=0 Radius=1.6
    g2: Circle CenterX=-28.7228 CenterY=35 CenterZ=0 NormalX=0 NormalY=0 NormalZ=1 AngleXU=0 Radius=1.6
  constraints (9):
    c: Radius(g0) = 35
    c: PointOnObject(g1,g0)
    c: PointOnObject(g2,g0)
    c: Equal(g2,g1)
    c: Radius(g2) = 1.6
    c: DistanceY(g1,g2) = 10
    c: DistanceY(g-1,g0) = 15
    c: DistanceY(g0,g1) = 10
    c: DistanceX(g0,g-1) = 0
FEATURE [PartDesign::Pocket] Pocket615  label="Screwholes Montage007"
  BaseFeature = -> Pocket604
  Length = 3
  Length2 = 100
  Profile = -> Sketch1542
  Type = 0
FEATURE [Sketcher::SketchObject] Sketch1550
  MapMode = 5
  Placement = pos=(0,0,5) rot=(0,0,1;0rad)
  Support = -> [Pocket615]
  sketch-geometry (1):
    g0: Circle CenterX=0 CenterY=0 CenterZ=0 NormalX=0 NormalY=0 NormalZ=1 AngleXU=0 Radius=6.15
  constraints (2):
    c: Coincident(g0,g-1)
    c: Radius(g0) = 6.15
FEATURE [PartDesign::Pocket] Pocket600  label="Ball Bearing Flange003"
  BaseFeature = -> Pocket615
  Length = 5
  Length2 = 100
  Profile = -> Sketch1550
  Type = 0
FEATURE [Sketcher::SketchObject] Sketch1544
  MapMode = 5
  Placement = pos=(0,0,0) rot=(1,0,0;3.14159rad)
  Support = -> [Pocket600]
  sketch-geometry (1):
    g0: Circle CenterX=0 CenterY=0 CenterZ=0 NormalX=0 NormalY=0 NormalZ=1 AngleXU=0 Radius=8.15
  constraints (2):
    c: Coincident(g0,g-1)
    c: Radius(g0) = 8.15
FEATURE [PartDesign::Pocket] Pocket676  label="Ball Bearing Pocket003"
  BaseFeature = -> Pocket600
  Length = 4.5
  Length2 = 100
  Profile = -> Sketch1544
  Type = 0
FEATURE [PartDesign::Fillet] Fillet227  label="Ball Bearing Pocket Bottom Fillet003"
  Base = -> Pocket676 [Edge43]
  BaseFeature = -> Pocket676
  Radius = 1.8
FEATURE [PartDesign::Fillet] Fillet205  label="Smooth End Edge003"
  Base = -> Fillet227 [Edge31]
  BaseFeature = -> Fillet227
  Radius = 0.4
FEATURE [PartDesign::Pad] Pad815  label="M3x8 Thread100"
  BaseFeature = -> Pad687
  Length = 8
  Length2 = 100
  Profile = -> Sketch1669
  Type = 0
FEATURE [Sketcher::SketchObject] Sketch1679
  MapMode = 5
  Placement = pos=(0,0,0) rot=(1,0,0;3.14159rad)
  Support = -> [Pad815]
  sketch-geometry (7):
    g0: LineSegment StartX=0.77 StartY=0.44456 StartZ=0 EndX=0 EndY=0.889119 EndZ=0
    g1: LineSegment StartX=0 StartY=0.889119 StartZ=0 EndX=-0.77 EndY=0.44456 EndZ=0
    g2: LineSegment StartX=-0.77 StartY=0.44456 StartZ=0 EndX=-0.77 EndY=-0.44456 EndZ=0
    g3: LineSegment StartX=-0.77 StartY=-0.44456 StartZ=0 EndX=3.85628e-11 EndY=-0.889119 EndZ=0
    g4: LineSegment StartX=3.85628e-11 StartY=-0.889119 StartZ=0 EndX=0.77 EndY=-0.44456 EndZ=0
    g5: LineSegment StartX=0.77 StartY=-0.44456 StartZ=0 EndX=0.77 EndY=0.44456 EndZ=0
    g6: Circle [constr] CenterX=0 CenterY=0 CenterZ=0 NormalX=0 NormalY=0 NormalZ=1 AngleXU=0 Radius=0.889119
  constraints (16):
    c: Coincident(g0,g1)
    c: Coincident(g1,g2)
    c: Coincident(g2,g3)
    c: Coincident(g3,g4)
    c: Coincident(g4,g5)
    c: Coincident(g5,g0)
    c: Equal(g0, g1-g5) x5
    c: PointOnObject(g0,g6)
    c: PointOnObject(g1,g6)
    c: PointOnObject(g2,g6)
    c: PointOnObject(g3,g6)
    c: PointOnObject(g4,g6)
    c: PointOnObject(g5,g6)
    c: Coincident(g6,g-1)
    c: PointOnObject(g0,g-2)
    c: DistanceX(g1,g0) = 1.54
FEATURE [PartDesign::Pocket] Pocket683  label="M3x8 Wrench097"
  BaseFeature = -> Pad815
  Length = 1
  Length2 = 100
  Profile = -> Sketch1679
  Type = 0
FEATURE [PartDesign::Chamfer] Chamfer322  label="M3x8 Smooth084"
  Base = -> Pocket683 [Face11,Edge2,Edge24,Edge3]
  BaseFeature = -> Pocket683
  Size = 0.2
FEATURE [PartDesign::Pad] Pad816
  BaseFeature = -> Pocket661
  Length = 3
  Length2 = 100
  Profile = -> Sketch1728
  Type = 0
FEATURE [PartDesign::Fillet] Fillet199
  Base = -> Pad816 [Face5,Edge96,Face4]
  BaseFeature = -> Pad816
  Radius = 0.2
FEATURE [PartDesign::Pad] Pad817  label="M3x8 Head100"
  Length = 2
  Length2 = 100
  Profile = -> Sketch1668
  Type = 0
FEATURE [Sketcher::SketchObject] Sketch1666
  MapMode = 5
  Placement = pos=(0,0,2) rot=(0,0,1;0rad)
  Support = -> [Pad817]
  sketch-geometry (1):
    g0: Circle CenterX=0 CenterY=0 CenterZ=0 NormalX=0 NormalY=0 NormalZ=1 AngleXU=0 Radius=1
  constraints (2):
    c: Coincident(g0,g-1)
    c: Radius(g0) = 1
FEATURE [PartDesign::Pad] Pad808  label="M3x8 Thread098"
  BaseFeature = -> Pad817
  Length = 8
  Length2 = 100
  Profile = -> Sketch1666
  Type = 0
FEATURE [Sketcher::SketchObject] Sketch1670
  MapMode = 5
  Placement = pos=(0,0,0) rot=(1,0,0;3.14159rad)
  Support = -> [Pad808]
  sketch-geometry (7):
    g0: LineSegment StartX=0.77 StartY=0.44456 StartZ=0 EndX=0 EndY=0.889119 EndZ=0
    g1: LineSegment StartX=0 StartY=0.889119 StartZ=0 EndX=-0.77 EndY=0.44456 EndZ=0
    g2: LineSegment StartX=-0.77 StartY=0.44456 StartZ=0 EndX=-0.77 EndY=-0.44456 EndZ=0
    g3: LineSegment StartX=-0.77 StartY=-0.44456 StartZ=0 EndX=3.85628e-11 EndY=-0.889119 EndZ=0
    g4: LineSegment StartX=3.85628e-11 StartY=-0.889119 StartZ=0 EndX=0.77 EndY=-0.44456 EndZ=0
    g5: LineSegment StartX=0.77 StartY=-0.44456 StartZ=0 EndX=0.77 EndY=0.44456 EndZ=0
    g6: Circle [constr] CenterX=0 CenterY=0 CenterZ=0 NormalX=0 NormalY=0 NormalZ=1 AngleXU=0 Radius=0.889119
  constraints (16):
    c: Coincident(g0,g1)
    c: Coincident(g1,g2)
    c: Coincident(g2,g3)
    c: Coincident(g3,g4)
    c: Coincident(g4,g5)
    c: Coincident(g5,g0)
    c: Equal(g0, g1-g5) x5
    c: PointOnObject(g0,g6)
    c: PointOnObject(g1,g6)
    c: PointOnObject(g2,g6)
    c: PointOnObject(g3,g6)
    c: PointOnObject(g4,g6)
    c: PointOnObject(g5,g6)
    c: Coincident(g6,g-1)
    c: PointOnObject(g0,g-2)
    c: DistanceX(g1,g0) = 1.54
FEATURE [PartDesign::Pocket] Pocket598  label="M3x8 Wrench089"
  BaseFeature = -> Pad808
  Length = 1
  Length2 = 100
  Profile = -> Sketch1670
  Type = 0
FEATURE [PartDesign::Chamfer] Chamfer360  label="M3x8 Smooth092"
  Base = -> Pocket598 [Face11,Edge2,Edge24,Edge3]
  BaseFeature = -> Pocket598
  Size = 0.2
FEATURE [PartDesign::Groove] Groove171  label="M3 Nut Smooth163"
  Angle = 360
  Axis = (-2e-16,3e-16,1)
  Base = (0,0,0)
  BaseFeature = -> Pad702
  Profile = -> Sketch1600
  ReferenceAxis = -> Sketch1600 [V_Axis]
  Reversed = true
FEATURE [PartDesign::Chamfer] Chamfer344  label="M3 Nut Smooth Hole144"
  Base = -> Groove171 [Edge24,Edge23]
  BaseFeature = -> Groove171
  Size = 0.2
FEATURE [PartDesign::Pad] Pad820
  Length = 10
  Length2 = 100
  Placement = pos=(0,0,0) rot=(1,0,0;1.5708rad)
  Profile = -> Sketch1569
  Reversed = true
  Type = 0
FEATURE [PartDesign::Pad] Pad822
  Length = 10
  Length2 = 100
  Placement = pos=(0,0,0) rot=(1,0,0;1.5708rad)
  Profile = -> Sketch1559
  Reversed = true
  Type = 0
FEATURE [PartDesign::Pad] Pad823  label="Baseplate035"
  Length = 30
  Length2 = 100
  Profile = -> Sketch1815
  Type = 0
FEATURE [PartDesign::Pad] Pad824  label="Baseplate036"
  Length = 30
  Length2 = 100
  Profile = -> Sketch1564
  Type = 0
FEATURE [PartDesign::Pad] Pad825
  Length = 5
  Length2 = 100
  Profile = -> Sketch1575
  Type = 0
FEATURE [Sketcher::SketchObject] Sketch1567
  ExternalGeometry = -> [Pad825]
  MapMode = 5
  Placement = pos=(0,0,5) rot=(0,0,1;0rad)
  Support = -> [Pad825]
  sketch-geometry (1):
    g0: Circle CenterX=0 CenterY=10.15 CenterZ=0 NormalX=0 NormalY=0 NormalZ=1 AngleXU=0 Radius=1.5
  constraints (2):
    c: Coincident(g0,g-3)
    c: Radius(g0) = 1.5
FEATURE [PartDesign::Pocket] Pocket620
  BaseFeature = -> Pad825
  Length = 4
  Length2 = 100
  Profile = -> Sketch1567
  Type = 0
FEATURE [PartDesign::Chamfer] Chamfer379
  Base = -> Pocket620 [Edge3]
  BaseFeature = -> Pocket620
  Size = 0.25
FEATURE [PartDesign::Pad] Pad826
  BaseFeature = -> Pad721
  Length = 0.5
  Length2 = 100
  Profile = -> Sketch1665
  Type = 0
FEATURE [Sketcher::SketchObject] Sketch1560
  ExternalGeometry = -> [Pad826]
  MapMode = 5
  Placement = pos=(0,0,39.1) rot=(0,0,1;0rad)
  Support = -> [Pad826]
  sketch-geometry (1):
    g0: Circle CenterX=0 CenterY=10.15 CenterZ=0 NormalX=0 NormalY=0 NormalZ=1 AngleXU=0 Radius=3
  constraints (2):
    c: Coincident(g0,g-3)
    c: Radius(g0) = 3
FEATURE [PartDesign::Pad] Pad730
  BaseFeature = -> Pad826
  Length = 4
  Length2 = 100
  Profile = -> Sketch1560
  Type = 0
FEATURE [Sketcher::SketchObject] Sketch1595
  ExternalGeometry = -> [Pad730]
  MapMode = 5
  Placement = pos=(0,0,43.1) rot=(0,0,1;0rad)
  Support = -> [Pad730]
  sketch-geometry (1):
    g0: Circle CenterX=0 CenterY=10.15 CenterZ=0 NormalX=0 NormalY=0 NormalZ=1 AngleXU=0 Radius=1.5
  constraints (2):
    c: Coincident(g0,g-3)
    c: Radius(g0) = 1.5
FEATURE [PartDesign::Pocket] Pocket690
  BaseFeature = -> Pad730
  Length = 5
  Length2 = 100
  Profile = -> Sketch1595
  Type = 0
FEATURE [Sketcher::SketchObject] Sketch1541
  MapMode = 5
  Placement = pos=(0,0,29.1) rot=(0,0,1;0rad)
  Support = -> [Pocket690]
  sketch-geometry (4):
    g0: Circle CenterX=-4.91157 CenterY=25.3 CenterZ=0 NormalX=0 NormalY=0 NormalZ=1 AngleXU=0 Radius=2.25
    g1: Circle CenterX=4.91157 CenterY=25.3 CenterZ=0 NormalX=0 NormalY=0 NormalZ=1 AngleXU=0 Radius=2.25
    g2: Circle CenterX=-4.91157 CenterY=-25.3 CenterZ=0 NormalX=0 NormalY=0 NormalZ=1 AngleXU=0 Radius=2.25
    g3: Circle CenterX=4.91157 CenterY=-25.3 CenterZ=0 NormalX=0 NormalY=0 NormalZ=1 AngleXU=0 Radius=2.25
  constraints (8):
    c: Equal(g3,g2)
    c: Equal(g2,g1)
    c: Equal(g1,g0)
    c: Radius(g1) = 2.25
    c: Symmetric(g1,g0,g-2)
    c: Symmetric(g3,g2,g-2)
    c: Symmetric(g3,g1,g-1)
    c: DistanceY(g3,g1) = 50.6
FEATURE [PartDesign::Pocket] Pocket624
  BaseFeature = -> Pocket690
  Length = 5
  Length2 = 100
  Profile = -> Sketch1541
  Type = 0
FEATURE [Sketcher::SketchObject] Sketch1565
  MapMode = 5
  Placement = pos=(0,0,29.1) rot=(0,0,1;0rad)
  Support = -> [Pocket624]
  sketch-geometry (8):
    g0: LineSegment StartX=-0.5 StartY=26.8 StartZ=0 EndX=0.5 EndY=26.8 EndZ=0
    g1: LineSegment StartX=0.5 StartY=26.8 StartZ=0 EndX=0.5 EndY=20.15 EndZ=0
    g2: LineSegment StartX=0.5 StartY=20.15 StartZ=0 EndX=-0.5 EndY=20.15 EndZ=0
    g3: LineSegment StartX=-0.5 StartY=20.15 StartZ=0 EndX=-0.5 EndY=26.8 EndZ=0
    g4: LineSegment StartX=-0.5 StartY=-20.15 StartZ=0 EndX=0.5 EndY=-20.15 EndZ=0
    g5: LineSegment StartX=0.5 StartY=-20.15 StartZ=0 EndX=0.5 EndY=-26.8 EndZ=0
    g6: LineSegment StartX=0.5 StartY=-26.8 StartZ=0 EndX=-0.5 EndY=-26.8 EndZ=0
    g7: LineSegment StartX=-0.5 StartY=-26.8 StartZ=0 EndX=-0.5 EndY=-20.15 EndZ=0
  constraints (20):
    c: Coincident(g0,g1)
    c: Coincident(g1,g2)
    c: Coincident(g2,g3)
    c: Coincident(g3,g0)
    c: Horizontal(g2)
    c: Vertical(g1)
    c: Vertical(g3)
    c: Coincident(g4,g5)
    c: Coincident(g5,g6)
    c: Coincident(g6,g7)
    c: Coincident(g7,g4)
    c: Horizontal(g6)
    c: Vertical(g7)
    c: Symmetric(g4,g4,g-2)
    c: Symmetric(g0,g0,g-2)
    c: Symmetric(g0,g5,g-1)
    c: DistanceY(g5,g0) = 53.6
    c: DistanceY(g4,g1) = 40.3
    c: DistanceX(g0,g0) = 1
    c: Symmetric(g4,g1,g-1)
FEATURE [PartDesign::Pocket] Pocket701
  BaseFeature = -> Pad790
  Length = 5
  Length2 = 100
  Profile = -> Sketch1745
  Type = 0
FEATURE [Sketcher::SketchObject] Sketch1751
  MapMode = 5
  Placement = pos=(0,0,0) rot=(1,0,0;3.14159rad)
  Support = -> [Pocket701]
  sketch-geometry (2):
    g0: Circle CenterX=0 CenterY=0 CenterZ=0 NormalX=0 NormalY=0 NormalZ=1 AngleXU=0 Radius=3.5
    g1: Circle CenterX=0 CenterY=0 CenterZ=0 NormalX=0 NormalY=0 NormalZ=1 AngleXU=0 Radius=7
  constraints (4):
    c: Coincident(g0,g-1)
    c: Coincident(g1,g0)
    c: Radius(g0) = 3.5
    c: Radius(g1) = 7
FEATURE [PartDesign::Pocket] Pocket682
  BaseFeature = -> Pocket701
  Length = 0.5
  Length2 = 100
  Profile = -> Sketch1751
  Type = 0
FEATURE [Sketcher::SketchObject] Sketch1748
  MapMode = 5
  Placement = pos=(0,0,5) rot=(0,0,1;0rad)
  Support = -> [Pocket682]
  sketch-geometry (2):
    g0: Circle CenterX=0 CenterY=0 CenterZ=0 NormalX=0 NormalY=0 NormalZ=1 AngleXU=0 Radius=3.5
    g1: Circle CenterX=0 CenterY=0 CenterZ=0 NormalX=0 NormalY=0 NormalZ=1 AngleXU=0 Radius=7
  constraints (4):
    c: Coincident(g0,g-1)
    c: Coincident(g1,g0)
    c: Radius(g0) = 3.5
    c: Radius(g1) = 7
FEATURE [PartDesign::Pocket] Pocket698
  BaseFeature = -> Pocket682
  Length = 0.5
  Length2 = 100
  Profile = -> Sketch1748
  Type = 0
FEATURE [PartDesign::Chamfer] Chamfer333
  Base = -> Pocket698 [Face10,Face2,Face3,Face11]
  BaseFeature = -> Pocket698
  Size = 0.25
FEATURE [PartDesign::Pad] Pad827
  BaseFeature = -> Pocket624
  Length = 2
  Length2 = 100
  Profile = -> Sketch1565
  Type = 0
FEATURE [Sketcher::SketchObject] Sketch1588
  ExternalGeometry = -> [Pad827]
  MapMode = 5
  Placement = pos=(0.5,0,0) rot=(0.57735,0.57735,0.57735;2.0944rad)
  Support = -> [Pad827]
  sketch-geometry (6):
    g0: LineSegment StartX=-26.8 StartY=29.1 StartZ=0 EndX=-26.8 EndY=31.1 EndZ=0
    g1: LineSegment StartX=-26.8 StartY=31.1 StartZ=0 EndX=-20.15 EndY=31.1 EndZ=0
    g2: LineSegment StartX=-20.15 StartY=31.1 StartZ=0 EndX=-26.8 EndY=29.1 EndZ=0
    g3: LineSegment StartX=20.15 StartY=31.1 StartZ=0 EndX=26.8 EndY=31.1 EndZ=0
    g4: LineSegment StartX=26.8 StartY=31.1 StartZ=0 EndX=26.8 EndY=29.1 EndZ=0
    g5: LineSegment StartX=26.8 StartY=29.1 StartZ=0 EndX=20.15 EndY=31.1 EndZ=0
  constraints (14):
    c: Vertical(g0)
    c: Coincident(g0,g1)
    c: Horizontal(g1)
    c: Coincident(g1,g2)
    c: Coincident(g2,g0)
    c: Coincident(g3,g4)
    c: Coincident(g4,g5)
    c: Coincident(g5,g3)
    c: Symmetric(g0,g4,g-2)
    c: Symmetric(g3,g0,g-2)
    c: Symmetric(g1,g3,g-2)
    c: DistanceX(g0,g3) = 53.6
    c: DistanceY(g4,g4) = 2
    c: Coincident(g3,g-3)
FEATURE [PartDesign::Pocket] Pocket700
  BaseFeature = -> Pad827
  Length = 1
  Length2 = 100
  Profile = -> Sketch1588
  Type = 0
FEATURE [PartDesign::Fillet] Fillet236
  Base = -> Pocket700 [Edge26,Edge27,Edge72,Edge63,Edge70,Edge78,Edge51,Edge49,Edge71,Edge50,Edge79,Edge86,Edge30,Edge21,Edge4,Edge29,Edge105,Edge107,Edge109,Edge111,Edge113,Edge114,Edge123]
  BaseFeature = -> Pocket700
  Radius = 0.4
FEATURE [Sketcher::SketchObject] Sketch1568
  MapMode = 5
  Placement = pos=(0,20.15,0) rot=(0,0.707107,0.707107;3.14159rad)
  Support = -> [Fillet236]
  sketch-geometry (4):
    g0: LineSegment StartX=-3.25 StartY=2 StartZ=0 EndX=3.25 EndY=2 EndZ=0
    g1: LineSegment StartX=3.25 StartY=2 StartZ=0 EndX=3.25 EndY=6 EndZ=0
    g2: LineSegment StartX=3.25 StartY=6 StartZ=0 EndX=-3.25 EndY=6 EndZ=0
    g3: LineSegment StartX=-3.25 StartY=6 StartZ=0 EndX=-3.25 EndY=2 EndZ=0
  constraints (11):
    c: Coincident(g0,g1)
    c: Coincident(g1,g2)
    c: Coincident(g2,g3)
    c: Coincident(g3,g0)
    c: Horizontal(g0)
    c: Vertical(g1)
    c: Vertical(g3)
    c: DistanceY(g-1,g0) = 2
    c: DistanceY(g1,g1) = 4
    c: Symmetric(g2,g1,g-2)
    c: DistanceX(g2,g2) = 6.5
FEATURE [PartDesign::Pad] Pad828  label="M3 Nut Primitive163"
  Length = 1.2
  Length2 = 1.2
  Profile = -> Sketch1820
  Type = 4
FEATURE [Sketcher::SketchObject] Sketch1639
  ExternalGeometry = -> [Pad828]
  MapMode = 5
  Placement = pos=(0,0,0) rot=(0.57735,0.57735,0.57735;2.0944rad)
  Support = -> [YZ_Plane606]
  sketch-geometry (6):
    g0: LineSegment StartX=-2.67543 StartY=1.2 StartZ=0 EndX=-3.67543 EndY=1.2 EndZ=0
    g1: LineSegment StartX=-3.67543 StartY=1.2 StartZ=0 EndX=-3.67543 EndY=-1.2 EndZ=0
    g2: LineSegment StartX=-3.67543 StartY=-1.2 StartZ=0 EndX=-2.67543 EndY=-1.2 EndZ=0
    g3: LineSegment StartX=-2.67543 StartY=-1.2 StartZ=0 EndX=-3.17543 EndY=-1 EndZ=0
    g4: LineSegment StartX=-3.17543 StartY=-1 StartZ=0 EndX=-3.17543 EndY=1 EndZ=0
    g5: LineSegment StartX=-3.17543 StartY=1 StartZ=0 EndX=-2.67543 EndY=1.2 EndZ=0
  constraints (15):
    c: Horizontal(g0)
    c: Coincident(g0,g1)
    c: Coincident(g1,g2)
    c: Coincident(g2,g3)
    c: Coincident(g3,g4)
    c: Coincident(g4,g5)
    c: Coincident(g5,g0)
    c: Symmetric(g4,g3,g-1)
    c: Symmetric(g0,g2,g-1)
    c: Symmetric(g1,g0,g-1)
    c: DistanceX(g0,g4) = 0.5
    c: DistanceY(g3,g4) = 2
    c: DistanceY(g1,g0) = 2.4
    c: PointOnObject(g3,g-3)
    c: DistanceX(g4,g0) = 0.5
FEATURE [PartDesign::Groove] Groove166  label="M3 Nut Smooth158"
  Angle = 360
  Axis = (-2e-16,3e-16,1)
  Base = (0,0,0)
  BaseFeature = -> Pad828
  Profile = -> Sketch1639
  ReferenceAxis = -> Sketch1639 [V_Axis]
  Reversed = true
FEATURE [PartDesign::Chamfer] Chamfer324  label="M3 Nut Smooth Hole135"
  Base = -> Groove166 [Edge24,Edge23]
  BaseFeature = -> Groove166
  Size = 0.2
FEATURE [PartDesign::Pad] Pad829
  Length = 5
  Length2 = 100
  Profile = -> Sketch1744
  Type = 0
FEATURE [PartDesign::Chamfer] Chamfer341
  Base = -> Pad829 [Face3,Face4]
  BaseFeature = -> Pad829
  Size = 0.2
FEATURE [PartDesign::Pad] Pad830
  BaseFeature = -> Fillet236
  Length = 1
  Length2 = 100
  Profile = -> Sketch1568
  Type = 0
FEATURE [Sketcher::SketchObject] Sketch1580
  MapMode = 5
  Placement = pos=(0,21.15,0) rot=(0,0.707107,0.707107;3.14159rad)
  Support = -> [Pad830]
  sketch-geometry (4):
    g0: LineSegment StartX=-2.75 StartY=5.5 StartZ=0 EndX=2.75 EndY=5.5 EndZ=0
    g1: LineSegment StartX=2.75 StartY=5.5 StartZ=0 EndX=2.75 EndY=2.5 EndZ=0
    g2: LineSegment StartX=2.75 StartY=2.5 StartZ=0 EndX=-2.75 EndY=2.5 EndZ=0
    g3: LineSegment StartX=-2.75 StartY=2.5 StartZ=0 EndX=-2.75 EndY=5.5 EndZ=0
  constraints (11):
    c: Coincident(g0,g1)
    c: Coincident(g1,g2)
    c: Coincident(g2,g3)
    c: Coincident(g3,g0)
    c: Horizontal(g0)
    c: Vertical(g1)
    c: Vertical(g3)
    c: Symmetric(g1,g2,g-2)
    c: DistanceY(g1,g0) = 3
    c: DistanceY(g-1,g1) = 2.5
    c: DistanceX(g0,g0) = 5.5
FEATURE [PartDesign::Pad] Pad718
  BaseFeature = -> Pad830
  Length = 4
  Length2 = 100
  Profile = -> Sketch1580
  Type = 0
FEATURE [Sketcher::SketchObject] Sketch1554
  MapMode = 5
  Placement = pos=(0,0,0) rot=(1,0,0;3.14159rad)
  Support = -> [Pad718]
  sketch-geometry (4):
    g0: LineSegment StartX=-10 StartY=-20.15 StartZ=0 EndX=10 EndY=-20.15 EndZ=0
    g1: LineSegment StartX=10 StartY=-20.15 StartZ=0 EndX=10 EndY=20.15 EndZ=0
    g2: LineSegment StartX=10 StartY=20.15 StartZ=0 EndX=-10 EndY=20.15 EndZ=0
    g3: LineSegment StartX=-10 StartY=20.15 StartZ=0 EndX=-10 EndY=-20.15 EndZ=0
  constraints (10):
    c: Coincident(g0,g1)
    c: Coincident(g1,g2)
    c: Coincident(g2,g3)
    c: Coincident(g3,g0)
    c: Horizontal(g0)
    c: Vertical(g1)
    c: Symmetric(g2,g1,g-2)
    c: Symmetric(g0,g2,g-1)
    c: DistanceX(g2,g2) = 20
    c: DistanceY(g1,g1) = 40.3
FEATURE [PartDesign::Pad] Pad818
  BaseFeature = -> Pad718
  Length = 2
  Length2 = 100
  Profile = -> Sketch1554
  Type = 0
FEATURE [PartDesign::Chamfer] Chamfer306
  Base = -> Pad818 [Face7]
  BaseFeature = -> Pad818
  Size = 1.5
FEATURE [PartDesign::Fillet] Fillet211
  Base = -> Chamfer306 [Edge1,Edge7,Edge18,Edge4,Face12]
  BaseFeature = -> Chamfer306
  Radius = 0.4
FEATURE [Sketcher::SketchObject] Sketch1683
  ExternalGeometry = -> [Fillet211]
  MapMode = 5
  Placement = pos=(0,0,43.1) rot=(0,0,1;0rad)
  Support = -> [Fillet211]
  sketch-geometry (1):
    g0: Circle CenterX=0 CenterY=10.15 CenterZ=0 NormalX=0 NormalY=0 NormalZ=1 AngleXU=0 Radius=3
  constraints (2):
    c: Coincident(g0,g-3)
    c: Radius(g0) = 3
FEATURE [PartDesign::Pocket] Pocket702
  BaseFeature = -> Fillet211
  Length = 5
  Length2 = 100
  Profile = -> Sketch1683
  Type = 0
FEATURE [PartDesign::Pocket] Pocket703  label="Servohorn Mount Pocket006"
  BaseFeature = -> Pad824
  Length = 5
  Length2 = 100
  Profile = -> Pad824 [Face12]
  Type = 0
FEATURE [PartDesign::Pocket] Pocket663  label="Ball Bearing Mount Pocket006"
  BaseFeature = -> Pocket703
  Length = 5
  Length2 = 100
  Profile = -> Pocket703 [Face3]
  Type = 0
FEATURE [Sketcher::SketchObject] Sketch1811
  MapMode = 5
  Placement = pos=(40,0,0) rot=(0.57735,-0.57735,-0.57735;2.0944rad)
  Support = -> [Pocket663]
  sketch-geometry (6):
    g0: ArcOfCircle CenterX=-25.9999 CenterY=20 CenterZ=0 NormalX=0 NormalY=0 NormalZ=1 AngleXU=0 Radius=25.9999 StartAngle=6.28318 EndAngle=6.67798
    g1: LineSegment StartX=-2 StartY=30 StartZ=0 EndX=1 EndY=30 EndZ=0
    g2: LineSegment StartX=1 StartY=30 StartZ=0 EndX=1 EndY=0 EndZ=0
    g3: LineSegment StartX=1 StartY=0 StartZ=0 EndX=-2 EndY=2.39524e-11 EndZ=0
    g4: ArcOfCircle CenterX=-25.9999 CenterY=9.99999 CenterZ=0 NormalX=0 NormalY=0 NormalZ=1 AngleXU=0 Radius=25.9999 StartAngle=5.88839 EndAngle=6.28319
    g5: LineSegment StartX=-2.5011e-12 StartY=10 StartZ=0 EndX=-2.5011e-12 EndY=20 EndZ=0
  constraints (20):
    c: DistanceY(g0,g0) = 10
    c: DistanceX(g0,g-1) = 2
    c: Vertical(g0,g-1)
    c: Tangent(g0,g-2)
    c: DistanceY(g-1,g0) = 30
    c: Coincident(g0,g1)
    c: Coincident(g1,g2)
    c: PointOnObject(g2,g-1)
    c: Vertical(g2)
    c: Coincident(g2,g3)
    c: PointOnObject(g3,g-1)
    c: Coincident(g4,g3)
    c: Tangent(g4,g-2)
    c: Vertical(g3,g0)
    c: DistanceY(g-1,g4) = 10
    c: Coincident(g5,g4)
    c: Coincident(g5,g0)
    c: Vertical(g5)
    c: Horizontal(g1)
    c: DistanceX(g1,g1) = 3
FEATURE [PartDesign::SubtractivePipe] SubtractivePipe017  label="Smooth Beveled Surfaces006"
  AuxilleryCurvelinear = true
  AuxillerySpineTangent = false
  BaseFeature = -> Pocket663
  Binormal = (0,0,0)
  Mode = 0
  Profile = -> Sketch1811
  Spine = -> Pocket663 [Edge21,Edge22,Edge23,Edge24,Edge25,Edge26,Edge27,Edge28,Edge29]
  SpineTangent = false
  Transformation = 0
  Transition = 0
FEATURE [PartDesign::Fillet] Fillet197  label="Smooth Edges017"
  Base = -> SubtractivePipe017 [Edge20,Edge5]
  BaseFeature = -> SubtractivePipe017
  Radius = 1.5
FEATURE [Sketcher::SketchObject] Sketch1824
  MapMode = 5
  Placement = pos=(0,5,0) rot=(1,0,0;1.5708rad)
  Support = -> [Fillet197]
  sketch-geometry (1):
    g0: Circle CenterX=0 CenterY=0 CenterZ=0 NormalX=0 NormalY=0 NormalZ=1 AngleXU=0 Radius=30
  constraints (2):
    c: Coincident(g0,g-1)
    c: Radius(g0) = 30
FEATURE [PartDesign::Pocket] Pocket664  label="Joint Pan006"
  BaseFeature = -> Fillet197
  Length = 47
  Length2 = 100
  Profile = -> Sketch1824
  Type = 0
FEATURE [Sketcher::SketchObject] Sketch1533
  ExternalGeometry = -> [Pocket664]
  MapMode = 5
  Placement = pos=(0,5,0) rot=(1,0,0;1.5708rad)
  Support = -> [Pocket664]
  sketch-geometry (7):
    g0: ArcOfCircle CenterX=23.5 CenterY=28.2018 CenterZ=0 NormalX=0 NormalY=0 NormalZ=1 AngleXU=0 Radius=1.79818 StartAngle=1.57079 EndAngle=2.66896
    g1: LineSegment StartX=21.8989 StartY=29.0204 StartZ=0 EndX=19.5977 EndY=24.5195 EndZ=0
    g2: ArcOfCircle CenterX=21.1988 CenterY=23.701 CenterZ=0 NormalX=0 NormalY=0 NormalZ=1 AngleXU=0 Radius=1.79818 StartAngle=2.66896 EndAngle=3.98266
    g3: Circle [constr] CenterX=0 CenterY=0 CenterZ=0 NormalX=0 NormalY=0 NormalZ=1 AngleXU=0 Radius=30
    g4: LineSegment StartX=23.5 StartY=30 StartZ=0 EndX=0 EndY=30 EndZ=0
    g5: LineSegment StartX=0 StartY=30 StartZ=0 EndX=0 EndY=22.3607 EndZ=0
    g6: LineSegment StartX=0 StartY=22.3607 StartZ=0 EndX=20 EndY=22.3607 EndZ=0
  constraints (19):
    c: Coincident(g3,g-1)
    c: Radius(g3) = 30
    c: Coincident(g4,g0)
    c: PointOnObject(g4,g3)
    c: Horizontal(g4)
    c: Tangent(g4,g0)
    c: Coincident(g5,g4)
    c: Vertical(g5)
    c: Tangent(g2,g3) = 1.5708
    c: Tangent(g2,g1) = -1.5708
    c: Tangent(g1,g0) = -1.5708
    c: DistanceX(g4,g4) = 23.5
    c: PointOnObject(g4,g-2)
    c: DistanceX(g5,g2) = 20
    c: Equal(g0,g2)
    c: Coincident(g6,g5)
    c: Coincident(g6,g2)
    c: Horizontal(g6)
    c: Horizontal(g-3,g0)
FEATURE [PartDesign::Pocket] Pocket695  label="Shortened Angled Top007"
  BaseFeature = -> Pocket664
  Length = 47
  Length2 = 100
  Profile = -> Sketch1533
  Type = 0
FEATURE [PartDesign::Pocket] Pocket704  label="Servoplacement Helper Pocket007"
  BaseFeature = -> Pocket695
  Length = 15
  Length2 = 100
  Profile = -> Sketch1816
  Type = 0
FEATURE [PartDesign::Pad] Pad819  label="Servoplacement Helper Pad006"
  BaseFeature = -> Pocket704
  Length = 5
  Length2 = 100
  Profile = -> Pocket704 [Face60]
  Type = 0
FEATURE [PartDesign::Fillet] Fillet193  label="Servoplacement Smooth Edges006"
  Base = -> Pad819 [Edge121,Edge125]
  BaseFeature = -> Pad819
  Radius = 0.4
FEATURE [Sketcher::SketchObject] Sketch1812
  MapMode = 5
  Placement = pos=(0,10,-2.2e-15) rot=(1,0,0;1.5708rad)
  Support = -> [Fillet193]
  sketch-geometry (4):
    g0: LineSegment StartX=76.5 StartY=25 StartZ=0 EndX=117 EndY=25 EndZ=0
    g1: LineSegment StartX=117 StartY=25 StartZ=0 EndX=117 EndY=5 EndZ=0
    g2: LineSegment StartX=117 StartY=5 StartZ=0 EndX=76.5 EndY=5 EndZ=0
    g3: LineSegment StartX=76.5 StartY=5 StartZ=0 EndX=76.5 EndY=25 EndZ=0
  constraints (12):
    c: Coincident(g0,g1)
    c: Coincident(g1,g2)
    c: Coincident(g2,g3)
    c: Coincident(g3,g0)
    c: Horizontal(g0)
    c: Horizontal(g2)
    c: Vertical(g1)
    c: Vertical(g3)
    c: DistanceX(g0,g0) = 40.5
    c: DistanceY(g3,g3) = 20
    c: DistanceY(g-1,g2) = 5
    c: DistanceX(g-1,g2) = 76.5
FEATURE [PartDesign::Pocket] Pocket688  label="Servo Pocket013"
  BaseFeature = -> Fillet193
  Length = 30
  Length2 = 100
  Profile = -> Sketch1812
  Type = 0
FEATURE [PartDesign::Fillet] Fillet213  label="Smooth Mount Edges006"
  Base = -> Pocket688 [Edge147,Edge146,Edge141,Edge152]
  BaseFeature = -> Pocket688
  Radius = 0.4
FEATURE [Sketcher::SketchObject] Sketch1587
  MapMode = 5
  Placement = pos=(0,0,30) rot=(0,0,1;0rad)
  Support = -> [Fillet213]
  sketch-geometry (4):
    g0: LineSegment StartX=0 StartY=0 StartZ=0 EndX=130 EndY=0 EndZ=0
    g1: LineSegment StartX=130 StartY=0 StartZ=0 EndX=130 EndY=57 EndZ=0
    g2: LineSegment StartX=130 StartY=57 StartZ=0 EndX=0 EndY=57 EndZ=0
    g3: LineSegment StartX=0 StartY=57 StartZ=0 EndX=0 EndY=0 EndZ=0
  constraints (11):
    c: Coincident(g0,g1)
    c: Coincident(g1,g2)
    c: Coincident(g2,g3)
    c: Coincident(g3,g0)
    c: Horizontal(g0)
    c: Horizontal(g2)
    c: Vertical(g1)
    c: Vertical(g3)
    c: Coincident(g0,g-1)
    c: DistanceY(g1,g1) = 57
    c: DistanceX(g2,g2) = 130
FEATURE [PartDesign::Pocket] Pocket659  label="Remove Top Surface003"
  BaseFeature = -> Fillet213
  Length = 5
  Length2 = 100
  Profile = -> Sketch1587
  Type = 0
FEATURE [Sketcher::SketchObject] Sketch1549
  MapMode = 5
  Placement = pos=(0,0,25) rot=(0,0,1;0rad)
  Support = -> [Pocket659]
  sketch-geometry (7):
    g0: LineSegment StartX=0 StartY=43 StartZ=0 EndX=120 EndY=43 EndZ=0
    g1: ArcOfCircle CenterX=120 CenterY=38 CenterZ=0 NormalX=0 NormalY=0 NormalZ=1 AngleXU=0 Radius=5 StartAngle=3e-16 EndAngle=1.5708
    g2: LineSegment StartX=125 StartY=38 StartZ=0 EndX=125 EndY=10 EndZ=0
    g3: LineSegment StartX=125 StartY=10 StartZ=0 EndX=130 EndY=10 EndZ=0
    g4: LineSegment StartX=130 StartY=10 StartZ=0 EndX=130 EndY=57 EndZ=0
    g5: LineSegment StartX=130 StartY=57 StartZ=0 EndX=0 EndY=57 EndZ=0
    g6: LineSegment StartX=0 StartY=57 StartZ=0 EndX=0 EndY=43 EndZ=0
  constraints (20):
    c: Horizontal(g0)
    c: Tangent(g0,g1) = 1.5708
    c: Tangent(g1,g2) = 1.5708
    c: Coincident(g2,g3)
    c: Horizontal(g3)
    c: Coincident(g3,g4)
    c: Coincident(g4,g5)
    c: Horizontal(g5)
    c: Coincident(g5,g6)
    c: Coincident(g6,g0)
    c: Vertical(g6)
    c: Vertical(g4)
    c: Vertical(g2)
    c: PointOnObject(g0,g-2)
    c: DistanceY(g-1,g5) = 57
    c: DistanceX(g5,g5) = 130
    c: DistanceY(g-1,g3) = 10
    c: DistanceX(g3,g3) = 5
    c: Radius(g1) = 5
    c: DistanceY(g2,g0) = 33
FEATURE [PartDesign::Pocket] Pocket694  label="Remove Shell003"
  BaseFeature = -> Pocket659
  Length = 25
  Length2 = 100
  Profile = -> Sketch1549
  Type = 0
FEATURE [Sketcher::SketchObject] Sketch1818
  MapMode = 5
  Placement = pos=(0,0,25) rot=(0,0,1;0rad)
  Support = -> [Pocket694]
  sketch-geometry (4):
    g0: LineSegment StartX=117 StartY=10 StartZ=0 EndX=125 EndY=10 EndZ=0
    g1: LineSegment StartX=125 StartY=10 StartZ=0 EndX=125 EndY=15 EndZ=0
    g2: LineSegment StartX=125 StartY=15 StartZ=0 EndX=117 EndY=15 EndZ=0
    g3: LineSegment StartX=117 StartY=15 StartZ=0 EndX=117 EndY=10 EndZ=0
  constraints (12):
    c: Coincident(g0,g1)
    c: Coincident(g1,g2)
    c: Coincident(g2,g3)
    c: Coincident(g3,g0)
    c: Horizontal(g0)
    c: Horizontal(g2)
    c: Vertical(g1)
    c: Vertical(g3)
    c: DistanceY(g1,g1) = 5
    c: DistanceX(g2,g2) = 8
    c: DistanceY(g-1,g0) = 10
    c: DistanceX(g-1,g2) = 117
FEATURE [PartDesign::Pocket] Pocket669  label="Remove Shell at Servopocket003"
  BaseFeature = -> Pocket694
  Length = 20
  Length2 = 100
  Profile = -> Sketch1818
  Type = 0
FEATURE [Sketcher::SketchObject] Sketch1540
  MapMode = 5
  Placement = pos=(125,0,0) rot=(0.57735,0.57735,0.57735;2.0944rad)
  Support = -> [Pocket669]
  sketch-geometry (4):
    g0: LineSegment StartX=29.5 StartY=25 StartZ=0 EndX=34.5 EndY=25 EndZ=0
    g1: LineSegment StartX=29.5 StartY=25 StartZ=0 EndX=29.5 EndY=11.5 EndZ=0
    g2: LineSegment StartX=34.5 StartY=25 StartZ=0 EndX=34.5 EndY=11.5 EndZ=0
    g3: ArcOfCircle CenterX=32 CenterY=11.5 CenterZ=0 NormalX=0 NormalY=0 NormalZ=1 AngleXU=0 Radius=2.5 StartAngle=3.14159 EndAngle=6.28319
  constraints (11):
    c: Horizontal(g0)
    c: Coincident(g1,g0)
    c: Vertical(g1)
    c: Coincident(g2,g0)
    c: Vertical(g2)
    c: Tangent(g3,g1) = -1.5708
    c: Tangent(g3,g2) = 1.5708
    c: DistanceX(g0,g0) = 5
    c: DistanceY(g-1,g3) = 11.5
    c: DistanceX(g-1,g3) = 32
    c: DistanceY(g-1,g0) = 25
FEATURE [PartDesign::Pocket] Pocket693  label="Servocable013"
  BaseFeature = -> Pocket669
  Length = 8
  Length2 = 100
  Profile = -> Sketch1540
  Type = 0
FEATURE [Sketcher::SketchObject] Sketch1581
  MapMode = 5
  Placement = pos=(125,0,0) rot=(0.57735,0.57735,0.57735;2.0944rad)
  Support = -> [Pocket693]
  sketch-geometry (8):
    g0: LineSegment StartX=18 StartY=22.9 StartZ=0 EndX=21 EndY=22.9 EndZ=0
    g1: LineSegment StartX=21 StartY=22.9 StartZ=0 EndX=21 EndY=17.1 EndZ=0
    g2: LineSegment StartX=21 StartY=17.1 StartZ=0 EndX=18 EndY=17.1 EndZ=0
    g3: LineSegment StartX=18 StartY=17.1 StartZ=0 EndX=18 EndY=22.9 EndZ=0
    g4: LineSegment StartX=18 StartY=12.9 StartZ=0 EndX=21 EndY=12.9 EndZ=0
    g5: LineSegment StartX=21 StartY=12.9 StartZ=0 EndX=21 EndY=7.1 EndZ=0
    g6: LineSegment StartX=21 StartY=7.1 StartZ=0 EndX=18 EndY=7.1 EndZ=0
    g7: LineSegment StartX=18 StartY=7.1 StartZ=0 EndX=18 EndY=12.9 EndZ=0
  constraints (24):
    c: Coincident(g0,g1)
    c: Coincident(g1,g2)
    c: Coincident(g2,g3)
    c: Coincident(g3,g0)
    c: Horizontal(g0)
    c: Horizontal(g2)
    c: Vertical(g1)
    c: Vertical(g3)
    c: Coincident(g4,g5)
    c: Coincident(g5,g6)
    c: Coincident(g6,g7)
    c: Coincident(g7,g4)
    c: Horizontal(g4)
    c: Horizontal(g6)
    c: Vertical(g5)
    c: Vertical(g7)
    c: Equal(g0,g4)
    c: Equal(g1,g5)
    c: Vertical(g4,g2)
    c: DistanceX(g-1,g6) = 18
    c: DistanceX(g6,g6) = 3
    c: DistanceY(g5,g5) = 5.8
    c: DistanceY(g4,g1) = 4.2
    c: DistanceY(g-1,g6) = 7.1
FEATURE [PartDesign::Pocket] Pocket689  label="Nutholes Servopocket003"
  BaseFeature = -> Pocket693
  Length = 56.5
  Length2 = 100
  Profile = -> Sketch1581
  Type = 0
FEATURE [Sketcher::SketchObject] Sketch1809
  MapMode = 5
  Placement = pos=(0,10,-2.2e-15) rot=(1,0,0;1.5708rad)
  Support = -> [Pocket689]
  sketch-geometry (4):
    g0: Circle CenterX=72.5 CenterY=20 CenterZ=0 NormalX=0 NormalY=0 NormalZ=1 AngleXU=0 Radius=1.6
    g1: Circle CenterX=72.5 CenterY=10 CenterZ=0 NormalX=0 NormalY=0 NormalZ=1 AngleXU=0 Radius=1.6
    g2: Circle CenterX=121 CenterY=20 CenterZ=0 NormalX=0 NormalY=0 NormalZ=1 AngleXU=0 Radius=1.6
    g3: Circle CenterX=121 CenterY=10 CenterZ=0 NormalX=0 NormalY=0 NormalZ=1 AngleXU=0 Radius=1.6
  constraints (12):
    c: Vertical(g3,g2)
    c: Vertical(g1,g0)
    c: Horizontal(g0,g2)
    c: Horizontal(g1,g3)
    c: Equal(g0,g1)
    c: Equal(g1,g2)
    c: Equal(g2,g3)
    c: Radius(g2) = 1.6
    c: DistanceY(g1,g0) = 10
    c: DistanceY(g-1,g1) = 10
    c: DistanceX(g1,g3) = 48.5
    c: DistanceX(g-1,g1) = 72.5
FEATURE [PartDesign::Pocket] Pocket625  label="Screwholes Servopocket006"
  BaseFeature = -> Pocket689
  Length = 18
  Length2 = 100
  Profile = -> Sketch1809
  Type = 0
FEATURE [Sketcher::SketchObject] Sketch1817
  MapMode = 5
  Placement = pos=(0,5,0) rot=(1,0,0;1.5708rad)
  Support = -> [Pocket625]
  sketch-geometry (3):
    g0: Circle [constr] CenterX=0 CenterY=0 CenterZ=0 NormalX=0 NormalY=0 NormalZ=1 AngleXU=0 Radius=35
    g1: Circle CenterX=33.541 CenterY=10 CenterZ=0 NormalX=0 NormalY=0 NormalZ=1 AngleXU=0 Radius=1.6
    g2: Circle CenterX=28.7228 CenterY=20 CenterZ=0 NormalX=0 NormalY=0 NormalZ=1 AngleXU=0 Radius=1.6
  constraints (8):
    c: Coincident(g0,g-1)
    c: Radius(g0) = 35
    c: PointOnObject(g1,g0)
    c: PointOnObject(g2,g0)
    c: Equal(g2,g1)
    c: Radius(g2) = 1.6
    c: DistanceY(g1,g2) = 10
    c: DistanceY(g-1,g1) = 10
FEATURE [PartDesign::Pocket] Pocket691  label="Screwholes Servohorn Mount007"
  BaseFeature = -> Pocket625
  Length = 20
  Length2 = 100
  Profile = -> Sketch1817
  Type = 0
FEATURE [Sketcher::SketchObject] Sketch1532
  MapMode = 5
  Placement = pos=(0,43,0) rot=(0,0.707107,0.707107;3.14159rad)
  Support = -> [Pocket691]
  sketch-geometry (3):
    g0: Circle [constr] CenterX=0 CenterY=0 CenterZ=0 NormalX=0 NormalY=0 NormalZ=1 AngleXU=0 Radius=35
    g1: Circle CenterX=-33.541 CenterY=10 CenterZ=0 NormalX=0 NormalY=0 NormalZ=1 AngleXU=0 Radius=1.6
    g2: Circle CenterX=-28.7228 CenterY=20 CenterZ=0 NormalX=0 NormalY=0 NormalZ=1 AngleXU=0 Radius=1.6
  constraints (8):
    c: Coincident(g0,g-1)
    c: Radius(g0) = 35
    c: PointOnObject(g1,g0)
    c: PointOnObject(g2,g0)
    c: Equal(g2,g1)
    c: Radius(g2) = 1.6
    c: DistanceY(g1,g2) = 10
    c: DistanceY(g-1,g1) = 10
FEATURE [PartDesign::Pocket] Pocket692  label="Screwholes Ball Bearing Mount003"
  BaseFeature = -> Pocket691
  Length = 10
  Length2 = 100
  Profile = -> Sketch1532
  Type = 0
FEATURE [Sketcher::SketchObject] Sketch1548
  MapMode = 5
  Placement = pos=(0,0,25) rot=(0,0,1;0rad)
  Support = -> [Pocket692]
  sketch-geometry (6):
    g0: LineSegment StartX=0 StartY=14 StartZ=0 EndX=40 EndY=14 EndZ=0
    g1: LineSegment StartX=40 StartY=14 StartZ=0 EndX=40 EndY=26 EndZ=0
    g2: LineSegment StartX=0 StartY=31 StartZ=0 EndX=0 EndY=14 EndZ=0
    g3: LineSegment StartX=40 StartY=26 StartZ=0 EndX=67.5 EndY=26 EndZ=0
    g4: LineSegment StartX=67.5 StartY=26 StartZ=0 EndX=67.5 EndY=31 EndZ=0
    g5: LineSegment StartX=67.5 StartY=31 StartZ=0 EndX=0 EndY=31 EndZ=0
  constraints (18):
    c: Coincident(g0,g1)
    c: Coincident(g2,g0)
    c: Horizontal(g0)
    c: Vertical(g1)
    c: Vertical(g2)
    c: PointOnObject(g0,g-2)
    c: DistanceY(g1,g2) = 17
    c: DistanceY(g-1,g0) = 14
    c: Horizontal(g3)
    c: Coincident(g4,g3)
    c: Vertical(g4)
    c: Horizontal(g5)
    c: Coincident(g4,g5)
    c: Coincident(g1,g3)
    c: Coincident(g5,g2)
    c: DistanceX(g-1,g4) = 67.5
    c: DistanceY(g4,g4) = 5
    c: DistanceX(g0,g0) = 40
FEATURE [PartDesign::Pocket] Pocket605  label="Interlock003"
  BaseFeature = -> Pocket692
  Length = 20
  Length2 = 100
  Profile = -> Sketch1548
  Type = 0
FEATURE [PartDesign::Pocket] Pocket677  label="Bottom Nuthole Ball Bearing Mount003"
  BaseFeature = -> Pocket605
  Length = 38
  Length2 = 100
  Profile = -> Sketch1546
  Reversed = true
  Type = 0
FEATURE [PartDesign::Pocket] Pocket699  label="Top Nuthole Ball Bearing Mount003"
  BaseFeature = -> Pocket677
  Length = 33
  Length2 = 100
  Profile = -> Sketch1807
  Reversed = true
  Type = 0
FEATURE [PartDesign::Fillet] Fillet207  label="Smooth Interlock007"
  Base = -> Pocket699 [Edge21,Edge15,Edge85,Edge118,Edge117,Edge116,Edge75,Edge13,Edge76,Edge178,Edge179,Edge88,Edge84,Edge83,Edge82,Edge81,Edge14,Edge72,Edge78,Edge87,Edge86]
  BaseFeature = -> Pocket699
  Radius = 0.4
FEATURE [PartDesign::Fillet] Fillet237  label="Smooth Servopocket003"
  Base = -> Fillet207 [Edge244,Edge256,Edge257,Edge246,Edge255]
  BaseFeature = -> Fillet207
  Radius = 1
FEATURE [PartDesign::Fillet] Fillet198  label="Smooth Servocable Edges007"
  Base = -> Fillet237 [Edge10,Edge199]
  BaseFeature = -> Fillet237
  Radius = 2.5
FEATURE [PartDesign::Pocket] Pocket705  label="Servohorn Mount Pocket007"
  BaseFeature = -> Pad823
  Length = 5
  Length2 = 100
  Profile = -> Pad823 [Face12]
  Type = 0
FEATURE [PartDesign::Pocket] Pocket666  label="Ball Bearing Mount Pocket007"
  BaseFeature = -> Pocket705
  Length = 5
  Length2 = 100
  Profile = -> Pocket705 [Face3]
  Type = 0
FEATURE [Sketcher::SketchObject] Sketch1583
  MapMode = 5
  Placement = pos=(40,0,0) rot=(0.57735,-0.57735,-0.57735;2.0944rad)
  Support = -> [Pocket666]
  sketch-geometry (6):
    g0: ArcOfCircle CenterX=-25.9999 CenterY=20 CenterZ=0 NormalX=0 NormalY=0 NormalZ=1 AngleXU=0 Radius=25.9999 StartAngle=6.28318 EndAngle=6.67798
    g1: LineSegment StartX=-2 StartY=30 StartZ=0 EndX=1 EndY=30 EndZ=0
    g2: LineSegment StartX=1 StartY=30 StartZ=0 EndX=1 EndY=0 EndZ=0
    g3: LineSegment StartX=1 StartY=0 StartZ=0 EndX=-2 EndY=2.39524e-11 EndZ=0
    g4: ArcOfCircle CenterX=-25.9999 CenterY=9.99999 CenterZ=0 NormalX=0 NormalY=0 NormalZ=1 AngleXU=0 Radius=25.9999 StartAngle=5.88839 EndAngle=6.28319
    g5: LineSegment StartX=-2.5011e-12 StartY=10 StartZ=0 EndX=-2.5011e-12 EndY=20 EndZ=0
  constraints (20):
    c: DistanceY(g0,g0) = 10
    c: DistanceX(g0,g-1) = 2
    c: Vertical(g0,g-1)
    c: Tangent(g0,g-2)
    c: DistanceY(g-1,g0) = 30
    c: Coincident(g0,g1)
    c: Coincident(g1,g2)
    c: PointOnObject(g2,g-1)
    c: Vertical(g2)
    c: Coincident(g2,g3)
    c: PointOnObject(g3,g-1)
    c: Coincident(g4,g3)
    c: Tangent(g4,g-2)
    c: Vertical(g3,g0)
    c: DistanceY(g-1,g4) = 10
    c: Coincident(g5,g4)
    c: Coincident(g5,g0)
    c: Vertical(g5)
    c: Horizontal(g1)
    c: DistanceX(g1,g1) = 3
FEATURE [PartDesign::SubtractivePipe] SubtractivePipe019  label="Smooth Beveled Surfaces007"
  AuxilleryCurvelinear = true
  AuxillerySpineTangent = false
  BaseFeature = -> Pocket666
  Binormal = (0,0,0)
  Mode = 0
  Profile = -> Sketch1583
  Spine = -> Pocket666 [Edge21,Edge22,Edge23,Edge24,Edge25,Edge26,Edge27,Edge28,Edge29]
  SpineTangent = false
  Transformation = 0
  Transition = 0
FEATURE [PartDesign::Fillet] Fillet219  label="Smooth Edges018"
  Base = -> SubtractivePipe019 [Edge20,Edge5]
  BaseFeature = -> SubtractivePipe019
  Radius = 1.5
FEATURE [Sketcher::SketchObject] Sketch1808
  MapMode = 5
  Placement = pos=(0,5,0) rot=(1,0,0;1.5708rad)
  Support = -> [Fillet219]
  sketch-geometry (1):
    g0: Circle CenterX=0 CenterY=0 CenterZ=0 NormalX=0 NormalY=0 NormalZ=1 AngleXU=0 Radius=30
  constraints (2):
    c: Coincident(g0,g-1)
    c: Radius(g0) = 30
FEATURE [PartDesign::Pocket] Pocket697  label="Joint Pan007"
  BaseFeature = -> Fillet219
  Length = 47
  Length2 = 100
  Profile = -> Sketch1808
  Type = 0
FEATURE [Sketcher::SketchObject] Sketch1821
  ExternalGeometry = -> [Pocket697]
  MapMode = 5
  Placement = pos=(0,5,0) rot=(1,0,0;1.5708rad)
  Support = -> [Pocket697]
  sketch-geometry (7):
    g0: ArcOfCircle CenterX=23.5 CenterY=28.2018 CenterZ=0 NormalX=0 NormalY=0 NormalZ=1 AngleXU=0 Radius=1.79818 StartAngle=1.57079 EndAngle=2.66896
    g1: LineSegment StartX=21.8989 StartY=29.0204 StartZ=0 EndX=19.5977 EndY=24.5195 EndZ=0
    g2: ArcOfCircle CenterX=21.1988 CenterY=23.701 CenterZ=0 NormalX=0 NormalY=0 NormalZ=1 AngleXU=0 Radius=1.79818 StartAngle=2.66896 EndAngle=3.98266
    g3: Circle [constr] CenterX=0 CenterY=0 CenterZ=0 NormalX=0 NormalY=0 NormalZ=1 AngleXU=0 Radius=30
    g4: LineSegment StartX=23.5 StartY=30 StartZ=0 EndX=0 EndY=30 EndZ=0
    g5: LineSegment StartX=0 StartY=30 StartZ=0 EndX=0 EndY=22.3607 EndZ=0
    g6: LineSegment StartX=0 StartY=22.3607 StartZ=0 EndX=20 EndY=22.3607 EndZ=0
  constraints (19):
    c: Coincident(g3,g-1)
    c: Radius(g3) = 30
    c: Coincident(g4,g0)
    c: PointOnObject(g4,g3)
    c: Horizontal(g4)
    c: Tangent(g4,g0)
    c: Coincident(g5,g4)
    c: Vertical(g5)
    c: Tangent(g2,g3) = 1.5708
    c: Tangent(g2,g1) = -1.5708
    c: Tangent(g1,g0) = -1.5708
    c: DistanceX(g4,g4) = 23.5
    c: PointOnObject(g4,g-2)
    c: DistanceX(g5,g2) = 20
    c: Equal(g0,g2)
    c: Coincident(g6,g5)
    c: Coincident(g6,g2)
    c: Horizontal(g6)
    c: Horizontal(g-3,g0)
FEATURE [PartDesign::Pocket] Pocket665  label="Shortened Angled Top006"
  BaseFeature = -> Pocket697
  Length = 47
  Length2 = 100
  Profile = -> Sketch1821
  Type = 0
FEATURE [PartDesign::Pocket] Pocket660  label="Servoplacement Helper Pocket006"
  BaseFeature = -> Pocket665
  Length = 15
  Length2 = 100
  Profile = -> Sketch1826
  Type = 0
FEATURE [PartDesign::Pad] Pad821  label="Servoplacement Helper Pad007"
  BaseFeature = -> Pocket660
  Length = 5
  Length2 = 100
  Profile = -> Pocket660 [Face60]
  Type = 0
FEATURE [PartDesign::Fillet] Fillet220  label="Servoplacement Smooth Edges007"
  Base = -> Pad821 [Edge121,Edge125]
  BaseFeature = -> Pad821
  Radius = 0.4
FEATURE [Sketcher::SketchObject] Sketch1746
  MapMode = 5
  Placement = pos=(0,10,-2.2e-15) rot=(1,0,0;1.5708rad)
  Support = -> [Fillet220]
  sketch-geometry (4):
    g0: LineSegment StartX=76.5 StartY=25 StartZ=0 EndX=117 EndY=25 EndZ=0
    g1: LineSegment StartX=117 StartY=25 StartZ=0 EndX=117 EndY=5 EndZ=0
    g2: LineSegment StartX=117 StartY=5 StartZ=0 EndX=76.5 EndY=5 EndZ=0
    g3: LineSegment StartX=76.5 StartY=5 StartZ=0 EndX=76.5 EndY=25 EndZ=0
  constraints (12):
    c: Coincident(g0,g1)
    c: Coincident(g1,g2)
    c: Coincident(g2,g3)
    c: Coincident(g3,g0)
    c: Horizontal(g0)
    c: Horizontal(g2)
    c: Vertical(g1)
    c: Vertical(g3)
    c: DistanceX(g0,g0) = 40.5
    c: DistanceY(g3,g3) = 20
    c: DistanceY(g-1,g2) = 5
    c: DistanceX(g-1,g2) = 76.5
FEATURE [PartDesign::Pocket] Pocket674  label="Servo Pocket012"
  BaseFeature = -> Fillet220
  Length = 30
  Length2 = 100
  Profile = -> Sketch1746
  Type = 0
FEATURE [PartDesign::Fillet] Fillet221  label="Smooth Mount Edges007"
  Base = -> Pocket674 [Edge147,Edge146,Edge141,Edge152]
  BaseFeature = -> Pocket674
  Radius = 0.4
FEATURE [Sketcher::SketchObject] Sketch1590
  MapMode = 5
  Placement = pos=(0,0,0) rot=(1,0,0;3.14159rad)
  Support = -> [Fillet221]
  sketch-geometry (11):
    g0: LineSegment StartX=0 StartY=-43.25 StartZ=0 EndX=120.25 EndY=-43.25 EndZ=0
    g1: ArcOfCircle CenterX=120.25 CenterY=-38.25 CenterZ=0 NormalX=0 NormalY=0 NormalZ=1 AngleXU=0 Radius=5 StartAngle=4.71239 EndAngle=6.28319
    g2: LineSegment StartX=125.25 StartY=-38.25 StartZ=0 EndX=125.25 EndY=-14.75 EndZ=0
    g3: LineSegment StartX=125.25 StartY=-14.75 StartZ=0 EndX=117 EndY=-14.75 EndZ=0
    g4: LineSegment StartX=117 StartY=-14.75 StartZ=0 EndX=117 EndY=0 EndZ=0
    g5: LineSegment StartX=117 StartY=0 StartZ=0 EndX=0 EndY=0 EndZ=0
    g6: LineSegment StartX=0 StartY=0 StartZ=0 EndX=0 EndY=-14.25 EndZ=0
    g7: LineSegment StartX=0 StartY=-14.25 StartZ=0 EndX=39.75 EndY=-14.25 EndZ=0
    g8: LineSegment StartX=39.75 StartY=-14.25 StartZ=0 EndX=39.75 EndY=-25.75 EndZ=0
    g9: LineSegment StartX=39.75 StartY=-25.75 StartZ=0 EndX=0 EndY=-25.75 EndZ=0
    g10: LineSegment StartX=0 StartY=-25.75 StartZ=0 EndX=0 EndY=-43.25 EndZ=0
  constraints (30):
    c: PointOnObject(g0,g-2)
    c: Horizontal(g0)
    c: Tangent(g0,g1) = -1.5708
    c: Tangent(g1,g2) = -1.5708
    c: Coincident(g2,g3)
    c: Coincident(g3,g4)
    c: Coincident(g4,g5)
    c: Coincident(g5,g-1)
    c: Coincident(g5,g6)
    c: Coincident(g10,g0)
    c: Horizontal(g3)
    c: Vertical(g4)
    c: Vertical(g2)
    c: Horizontal(g5)
    c: DistanceX(g5,g2) = 125.25
    c: Radius(g1) = 5
    c: DistanceY(g4,g4) = 14.75
    c: DistanceX(g3,g3) = 8.25
    c: DistanceY(g0,g4) = 43.25
    c: Horizontal(g7)
    c: Coincident(g7,g8)
    c: Vertical(g8)
    c: Coincident(g8,g9)
    c: Horizontal(g9)
    c: Coincident(g6,g7)
    c: Tangent(g6,g10)
    c: DistanceY(g8,g8) = 11.5
    c: DistanceX(g7,g7) = 39.75
    c: DistanceY(g6,g5) = 14.25
    c: Coincident(g9,g10)
FEATURE [PartDesign::Pocket] Pocket633  label="Bottom Removal and Interlock003"
  BaseFeature = -> Fillet221
  Length = 25
  Length2 = 100
  Profile = -> Sketch1590
  Type = 0
FEATURE [Sketcher::SketchObject] Sketch1813
  MapMode = 5
  Placement = pos=(0,0,0) rot=(1,0,0;3.14159rad)
  Support = -> [Pocket633]
  sketch-geometry (4):
    g0: LineSegment StartX=0 StartY=-26 StartZ=0 EndX=40 EndY=-26 EndZ=0
    g1: LineSegment StartX=40 StartY=-26 StartZ=0 EndX=40 EndY=-14 EndZ=0
    g2: LineSegment StartX=40 StartY=-14 StartZ=0 EndX=0 EndY=-14 EndZ=0
    g3: LineSegment StartX=0 StartY=-14 StartZ=0 EndX=0 EndY=-26 EndZ=0
  constraints (12):
    c: Coincident(g0,g1)
    c: Coincident(g1,g2)
    c: Coincident(g2,g3)
    c: Coincident(g3,g0)
    c: Horizontal(g0)
    c: Horizontal(g2)
    c: Vertical(g1)
    c: Vertical(g3)
    c: PointOnObject(g0,g-2)
    c: DistanceY(g1,g1) = 12
    c: DistanceY(g2,g-1) = 14
    c: DistanceX(g0,g0) = 40
FEATURE [PartDesign::Pocket] Pocket667  label="Shorten Interlock003"
  BaseFeature = -> Pocket633
  Length = 5
  Length2 = 100
  Profile = -> Sketch1813
  Type = 0
FEATURE [Sketcher::SketchObject] Sketch1750
  MapMode = 5
  Placement = pos=(0,52,0) rot=(0,0.707107,0.707107;3.14159rad)
  Support = -> [Pocket667]
  sketch-geometry (3):
    g0: Circle [constr] CenterX=0 CenterY=0 CenterZ=0 NormalX=0 NormalY=0 NormalZ=1 AngleXU=0 Radius=35
    g1: Circle CenterX=-28.7228 CenterY=20 CenterZ=0 NormalX=0 NormalY=0 NormalZ=1 AngleXU=0 Radius=1.6
    g2: Circle CenterX=-33.541 CenterY=10 CenterZ=0 NormalX=0 NormalY=0 NormalZ=1 AngleXU=0 Radius=1.6
  constraints (8):
    c: Coincident(g0,g-1)
    c: Radius(g0) = 35
    c: PointOnObject(g1,g0)
    c: PointOnObject(g2,g0)
    c: Equal(g2,g1)
    c: Radius(g1) = 1.6
    c: DistanceY(g2,g1) = 10
    c: DistanceY(g-1,g2) = 10
FEATURE [PartDesign::Pocket] Pocket696  label="Screwholes Ball Bearing Mount (Interlock)003"
  BaseFeature = -> Pocket667
  Length = 22
  Length2 = 100
  Profile = -> Sketch1750
  Type = 0
FEATURE [Sketcher::SketchObject] Sketch1814
  MapMode = 5
  Placement = pos=(0,14.25,0) rot=(1,0,0;1.5708rad)
  Support = -> [Pocket696]
  sketch-geometry (3):
    g0: Circle [constr] CenterX=0 CenterY=0 CenterZ=0 NormalX=0 NormalY=0 NormalZ=1 AngleXU=0 Radius=35
    g1: Circle CenterX=28.7228 CenterY=20 CenterZ=0 NormalX=0 NormalY=0 NormalZ=1 AngleXU=0 Radius=1.6
    g2: Circle CenterX=33.541 CenterY=10 CenterZ=0 NormalX=0 NormalY=0 NormalZ=1 AngleXU=0 Radius=1.6
  constraints (8):
    c: Coincident(g0,g-1)
    c: PointOnObject(g1,g0)
    c: PointOnObject(g2,g0)
    c: Equal(g2,g1)
    c: Radius(g1) = 1.6
    c: DistanceY(g2,g1) = 10
    c: DistanceY(g-1,g2) = 10
    c: Radius(g0) = 35
FEATURE [PartDesign::Pocket] Pocket662  label="Screwholes Servohorn Mount006"
  BaseFeature = -> Pocket696
  Length = 10
  Length2 = 100
  Profile = -> Sketch1814
  Type = 0
FEATURE [PartDesign::Pocket] Pocket670  label="Bottom Nuthole Ball Bearing Mount (Interlock)003"
  BaseFeature = -> Pocket662
  Length = 38
  Length2 = 100
  Profile = -> Sketch1755
  Reversed = true
  Type = 0
FEATURE [PartDesign::Pocket] Pocket632  label="Top Nuthole Ball Bearing Mount (Interlock)003"
  BaseFeature = -> Pocket670
  Length = 33
  Length2 = 100
  Profile = -> Sketch1823
  Reversed = true
  Type = 0
FEATURE [Sketcher::SketchObject] Sketch1756
  MapMode = 5
  Placement = pos=(0,10,-2.2e-15) rot=(1,0,0;1.5708rad)
  Support = -> [Pocket632]
  sketch-geometry (2):
    g0: Circle CenterX=121 CenterY=20 CenterZ=0 NormalX=0 NormalY=0 NormalZ=1 AngleXU=0 Radius=1.6
    g1: Circle CenterX=121 CenterY=10 CenterZ=0 NormalX=0 NormalY=0 NormalZ=1 AngleXU=0 Radius=1.6
  constraints (6):
    c: Vertical(g1,g0)
    c: Equal(g0,g1)
    c: Radius(g0) = 1.6
    c: DistanceY(g1,g0) = 10
    c: DistanceX(g-1,g1) = 121
    c: DistanceY(g-1,g1) = 10
FEATURE [PartDesign::Pocket] Pocket675  label="Screwholes Servopocket007"
  BaseFeature = -> Pocket632
  Length = 6
  Length2 = 100
  Profile = -> Sketch1756
  Type = 0
FEATURE [Sketcher::SketchObject] Sketch1822
  MapMode = 5
  Placement = pos=(0,0,25) rot=(1,0,0;3.14159rad)
  Support = -> [Pocket675]
  sketch-geometry (4):
    g0: LineSegment StartX=125 StartY=-26 StartZ=0 EndX=125 EndY=-34.5 EndZ=0
    g1: LineSegment StartX=125 StartY=-34.5 StartZ=0 EndX=30 EndY=-34.5 EndZ=0
    g2: LineSegment StartX=30 StartY=-26 StartZ=0 EndX=125 EndY=-26 EndZ=0
    g3: LineSegment StartX=30 StartY=-34.5 StartZ=0 EndX=30 EndY=-26 EndZ=0
  constraints (12):
    c: Coincident(g0,g1)
    c: Horizontal(g1)
    c: Vertical(g0)
    c: DistanceX(g-1,g0) = 125
    c: Coincident(g3,g2)
    c: Horizontal(g2)
    c: Vertical(g3)
    c: DistanceY(g3,g3) = 8.5
    c: DistanceY(g2,g-1) = 26
    c: DistanceX(g-1,g2) = 30
    c: Coincident(g3,g1)
    c: Coincident(g0,g2)
FEATURE [PartDesign::Pocket] Pocket668  label="Cableguide003"
  BaseFeature = -> Pocket675
  Length = 2
  Length2 = 100
  Profile = -> Sketch1822
  Type = 0
FEATURE [PartDesign::Fillet] Fillet224  label="Smooth Corners Cableguide003"
  Base = -> Pocket668 [Edge183,Edge184,Edge188,Edge186]
  BaseFeature = -> Pocket668
  Radius = 1
FEATURE [PartDesign::Fillet] Fillet203  label="Smooth Interlock006"
  Base = -> Fillet224 [Edge89,Edge85,Edge79,Edge86,Edge78,Edge148,Edge80,Edge87,Edge27,Edge23,Edge25,Edge84]
  BaseFeature = -> Fillet224
  Radius = 0.2
FEATURE [Sketcher::SketchObject] Sketch1753
  MapMode = 5
  Placement = pos=(130,0,0) rot=(0.57735,0.57735,0.57735;2.0944rad)
  Support = -> [Fillet203]
  sketch-geometry (9):
    g0: LineSegment StartX=30.75 StartY=19.75 StartZ=0 EndX=33.25 EndY=19.75 EndZ=0
    g1: LineSegment StartX=34.5 StartY=18.5 StartZ=0 EndX=34.5 EndY=11.5 EndZ=0
    g2: LineSegment StartX=33.25 StartY=10.25 StartZ=0 EndX=30.75 EndY=10.25 EndZ=0
    g3: LineSegment StartX=29.5 StartY=11.5 StartZ=0 EndX=29.5 EndY=18.5 EndZ=0
    g4: ArcOfCircle CenterX=30.75 CenterY=18.5 CenterZ=0 NormalX=0 NormalY=0 NormalZ=1 AngleXU=0 Radius=1.25 StartAngle=1.5708 EndAngle=3.14159
    g5: ArcOfCircle CenterX=33.25 CenterY=18.5 CenterZ=0 NormalX=0 NormalY=0 NormalZ=1 AngleXU=0 Radius=1.25 StartAngle=1e-16 EndAngle=1.5708
    g6: ArcOfCircle CenterX=33.25 CenterY=11.5 CenterZ=0 NormalX=0 NormalY=0 NormalZ=1 AngleXU=0 Radius=1.25 StartAngle=4.71239 EndAngle=6.28319
    g7: ArcOfCircle CenterX=30.75 CenterY=11.5 CenterZ=0 NormalX=0 NormalY=0 NormalZ=1 AngleXU=0 Radius=1.25 StartAngle=3.14159 EndAngle=4.71239
    g8: Circle [constr] CenterX=32 CenterY=15 CenterZ=0 NormalX=0 NormalY=0 NormalZ=1 AngleXU=0 Radius=2.5
  constraints (23):
    c: Horizontal(g0)
    c: Horizontal(g2)
    c: Vertical(g1)
    c: Vertical(g3)
    c: Tangent(g3,g4) = 1.5708
    c: Tangent(g0,g4) = 1.5708
    c: Tangent(g0,g5) = 1.5708
    c: Tangent(g1,g5) = 1.5708
    c: Tangent(g1,g6) = 1.5708
    c: Tangent(g2,g6) = 1.5708
    c: Tangent(g3,g7) = 1.5708
    c: Tangent(g2,g7) = 1.5708
    c: DistanceY(g2,g0) = 9.5
    c: DistanceX(g3,g1) = 5
    c: Tangent(g8,g3)
    c: Tangent(g8,g1)
    c: Equal(g5,g4)
    c: Equal(g4,g7)
    c: Equal(g7,g6)
    c: Radius(g5) = 1.25
    c: DistanceY(g8,g0) = 4.75
    c: DistanceX(g-1,g8) = 32
    c: DistanceY(g-1,g8) = 15
FEATURE [PartDesign::Pocket] Pocket634  label="Servocable011"
  BaseFeature = -> Fillet203
  Length = 5
  Length2 = 100
  Profile = -> Sketch1753
  Type = 0
FEATURE [Sketcher::SketchObject] Sketch1754
  MapMode = 5
  Placement = pos=(0,0,0) rot=(1,0,0;3.14159rad)
  Support = -> [Pocket634]
  sketch-geometry (4):
    g0: LineSegment StartX=117 StartY=-15 StartZ=0 EndX=125.25 EndY=-15 EndZ=0
    g1: LineSegment StartX=125.25 StartY=-15 StartZ=0 EndX=125.25 EndY=-10 EndZ=0
    g2: LineSegment StartX=125.25 StartY=-10 StartZ=0 EndX=117 EndY=-10 EndZ=0
    g3: LineSegment StartX=117 StartY=-10 StartZ=0 EndX=117 EndY=-15 EndZ=0
  constraints (12):
    c: Coincident(g0,g1)
    c: Coincident(g1,g2)
    c: Coincident(g2,g3)
    c: Coincident(g3,g0)
    c: Horizontal(g0)
    c: Horizontal(g2)
    c: Vertical(g1)
    c: Vertical(g3)
    c: DistanceX(g2,g2) = 8.25
    c: DistanceY(g3,g3) = 5
    c: DistanceY(g2,g-1) = 10
    c: DistanceX(g-1,g2) = 117
FEATURE [PartDesign::Pocket] Pocket571  label="Servopocket Interlock003"
  BaseFeature = -> Pocket634
  Length = 5
  Length2 = 100
  Profile = -> Sketch1754
  Type = 0
FEATURE [PartDesign::PolarPattern] PolarPattern003  label="Horizontal Profile Polar Pattern003"
  Angle = 180
  Axis = -> Sketch1682 [N_Axis]
  BaseFeature = -> SubtractivePipe018
  Occurrences = 12
  Originals = -> [SubtractivePipe018]
  Placement = pos=(0,0,0) rot=(1,0,0;1.5708rad)
  Reversed = true
FEATURE [PartDesign::Groove] Groove143  label="Vertical Profiles003"
  Angle = 360
  Axis = (0,1,0)
  Base = (0,0,0)
  BaseFeature = -> PolarPattern003
  Placement = pos=(0,0,0) rot=(1,0,0;1.5708rad)
  Profile = -> Sketch1607
  ReferenceAxis = -> Sketch1607 [V_Axis]
FEATURE [PartDesign::Pocket] Pocket592  label="Cut Sides003"
  BaseFeature = -> Groove143
  Length = 25
  Length2 = 100
  Placement = pos=(0,0,0) rot=(1,0,0;1.5708rad)
  Profile = -> Sketch1537
  Reversed = true
  Type = 0
FEATURE [PartDesign::Pocket] Pocket590  label="Inner Halfspherical Cutout003"
  BaseFeature = -> Pocket592
  Length = 10
  Length2 = 10
  Placement = pos=(0,0,0) rot=(1,0,0;1.5708rad)
  Profile = -> Sketch1610
  Type = 4
FEATURE [PartDesign::Pocket] Pocket589  label="Slanted Edge003"
  BaseFeature = -> Pocket590
  Length = 15
  Length2 = 15
  Placement = pos=(0,0,0) rot=(1,0,0;1.5708rad)
  Profile = -> Sketch1601
  Type = 4
FEATURE [PartDesign::Pocket] Pocket626  label="Screwholes007"
  BaseFeature = -> Pocket589
  Length = 15
  Length2 = 15
  Placement = pos=(0,0,0) rot=(1,0,0;1.5708rad)
  Profile = -> Sketch1605
  Type = 4
FEATURE [Sketcher::SketchObject] Sketch1591
  ExternalGeometry = -> [Pocket626]
  MapMode = 5
  Placement = pos=(0,14,-6.2e-15) rot=(-1,0,0;1.5708rad)
  Support = -> [Pocket626]
  sketch-geometry (1):
    g0: Circle CenterX=0 CenterY=-3.34863 CenterZ=0 NormalX=0 NormalY=0 NormalZ=1 AngleXU=0 Radius=2.85
  constraints (2):
    c: Coincident(g0,g-3)
    c: Radius(g0) = 2.85
FEATURE [PartDesign::Pocket] Pocket611  label="Screwhead Left003"
  BaseFeature = -> Pocket626
  Length = 2.5
  Length2 = 100
  Placement = pos=(0,0,0) rot=(1,0,0;1.5708rad)
  Profile = -> Sketch1591
  Type = 0
FEATURE [Sketcher::SketchObject] Sketch1617
  ExternalGeometry = -> [Pocket611]
  MapMode = 5
  Placement = pos=(0,-14,6.2e-15) rot=(1,0,0;1.5708rad)
  Support = -> [Pocket611]
  sketch-geometry (1):
    g0: Circle CenterX=0 CenterY=3.34863 CenterZ=0 NormalX=0 NormalY=0 NormalZ=1 AngleXU=0 Radius=2.85
  constraints (2):
    c: Coincident(g-3,g0)
    c: Radius(g0) = 2.85
FEATURE [PartDesign::Pocket] Pocket607  label="Screwhead Right003"
  BaseFeature = -> Pocket611
  Length = 2.5
  Length2 = 100
  Placement = pos=(0,0,0) rot=(1,0,0;1.5708rad)
  Profile = -> Sketch1617
  Type = 0
FEATURE [PartDesign::Body] Body412  label="M2 Nut054"
  Group = -> [Sketch1543,Pad707,Sketch1892,Groove144,Chamfer335]
  Origin = -> Origin682
  Placement = pos=(-115.141,-152.75,71.5896) rot=(0.677661,0.519988,-0.519988;1.95044rad)
  Tip = -> Chamfer335
FEATURE [PartDesign::Body] Body413  label="Limb_Top_Shell003"
  Group = -> [Sketch1815,Pad823,Pocket705,Pocket666,Sketch1583,SubtractivePipe019,Fillet219,Sketch1808,Pocket697,Sketch1821,Pocket665,Sketch1826,Pocket660,Pad821,Fillet220,Sketch1746,Pocket674,Fillet221,Sketch1590,Pocket633,Sketch1813,Pocket667,Sketch1750,Pocket696,Sketch1814,Pocket662,Sketch1755,Pocket670,Sketch1823,Pocket632,Sketch1756,Pocket675,Sketch1822,Pocket668,Fillet224,Fillet203,Sketch1753,Pocket634,+2 more]
  Origin = -> Origin677
  Placement = pos=(-144.1,-29.45,42.1) rot=(0,0,1;0rad)
  Tip = -> Pocket571
FEATURE [Part::Mirroring] Part__Mirroring014  label="Limb_Top_Shell001 (Mirror #6)001"
  Base = (0,0,0)
  Normal = (0,0,1)
  Placement = pos=(0,-1.95,0) rot=(1,0,0;3.14159rad)
  Source = -> Body413
FEATURE [PartDesign::Body] Body414  label="Wrist_Counterpart003"
  Group = -> [Sketch1528,Pad712,Sketch1536,Pocket606,Sketch1902,Pocket601,Sketch1529,Pocket678,Sketch1538,Pocket618,Sketch1621,Pocket603,Fillet195,Sketch1614,Pocket609,Sketch1903,Pocket613,Fillet201,Fillet196,Sketch1527,Pad719,Fillet235]
  Origin = -> Origin666
  Placement = pos=(-115.966,-155,33.9411) rot=(0.382683,0,0.92388;3.14159rad)
  Tip = -> Fillet235
FEATURE [Part::Mirroring] Part__Mirroring008  label="Wrist_Counterpart001 (Mirror #3)001"
  Base = (0,0,0)
  Normal = (0,0,1)
  Placement = pos=(0,-309.85,3.8e-14) rot=(1,0,0;3.14159rad)
  Source = -> Body414
FEATURE [PartDesign::Body] Body415  label="M3 Nut074"
  Group = -> [Sketch1618,Pad702,Sketch1600,Groove171,Chamfer344]
  Origin = -> Origin650
  Placement = pos=(0.75,5.5,34.25) rot=(1,0,0;1.5708rad)
  Tip = -> Chamfer344
FEATURE [PartDesign::Body] Body416  label="M2x062"
  Group = -> [Sketch1663,Pad803,Sketch1737,Pad805,Sketch1741,Pocket684,Chamfer321]
  Origin = -> Origin575
  Tip = -> Chamfer321
FEATURE [PartDesign::Body] Body417  label="M2 Nut055"
  Group = -> [Sketch1667,Pad797,Sketch1723,Groove170,Chamfer388,Sketch1722,Sketch1736]
  Origin = -> Origin591
  Placement = pos=(0,0,2.75) rot=(0,0,1;0rad)
  Tip = -> Chamfer388
FEATURE [PartDesign::Body] Body418  label="M2 Nut056"
  Group = -> [Sketch1743,Pad704,Sketch1555,Groove140,Chamfer327,Sketch1562,Sketch1561]
  Origin = -> Origin589
  Placement = pos=(0,0,2.75) rot=(0,0,1;0rad)
  Tip = -> Chamfer327
FEATURE [PartDesign::Body] Body419  label="M2x063"
  Group = -> [Sketch1557,Pad689,Sketch1673,Pad694,Sketch1675,Pocket595,Chamfer308]
  Origin = -> Origin607
  Tip = -> Chamfer308
FEATURE [App::Part] Part194  label="M061"
  Group = -> [Body419,Body418]
  Origin = -> Origin701
  Placement = pos=(-9.1,5.25,80) rot=(0,1,0;3.14159rad)
FEATURE [PartDesign::Body] Body420  label="red wire012"
  Group = -> [Sketch1559,Pad822]
  Origin = -> Origin700
  Placement = pos=(0,25.15,0) rot=(0,0,1;0rad)
  Tip = -> Pad822
FEATURE [PartDesign::Body] Body421  label="Gear012"
  Group = -> [Sketch1575,Pad825,Sketch1567,Pocket620,Chamfer379]
  Origin = -> Origin733
  Placement = pos=(0,0,38.25) rot=(0,0,1;0rad)
  Tip = -> Chamfer379
FEATURE [PartDesign::Body] Body422  label="M2x064"
  Group = -> [Sketch1668,Pad817,Sketch1666,Pad808,Sketch1670,Pocket598,Chamfer360]
  Origin = -> Origin608
  Tip = -> Chamfer360
FEATURE [App::Part] Part165  label="M052"
  Group = -> [Body422,Body417]
  Origin = -> Origin597
  Placement = pos=(-9.1,-5.25,80) rot=(0,1,0;3.14159rad)
FEATURE [PartDesign::Body] Body423  label="M3x088"
  Group = -> [Sketch1802,Pad666,Sketch1659,Pad662,Sketch1632,Pocket636,Chamfer320]
  Origin = -> Origin660
  Placement = pos=(-110.55,-29.35,52.05) rot=(-1,0,0;1.5708rad)
  Tip = -> Chamfer320
FEATURE [PartDesign::Body] Body424  label="M3 Nut075"
  Group = -> [Sketch1810,Pad754,Sketch1616,Groove164,Chamfer303]
  Origin = -> Origin645
  Placement = pos=(-115.35,7.7,62.05) rot=(0.57735,0.57735,-0.57735;2.0944rad)
  Tip = -> Chamfer303
FEATURE [PartDesign::Body] Body425  label="M2 Nut057"
  Group = -> [Sketch1672,Pad692,Sketch1724,Groove142,Chamfer318,Sketch1677,Sketch1739]
  Origin = -> Origin632
  Placement = pos=(0,0,2.75) rot=(0,0,1;0rad)
  Tip = -> Chamfer318
FEATURE [PartDesign::Body] Body426  label="Futuba FSH6B008"
  Group = -> [Sketch1715,Pad804,Sketch1714,Pocket672,Sketch1719,Pocket671,Sketch1725,Pocket661,Sketch1728,Pad816,Fillet199]
  Origin = -> Origin673
  Tip = -> Fillet199
FEATURE [App::Part] Part180  label="Servohorn014"
  Group = -> [Body426]
  Origin = -> Origin600
  Placement = pos=(0,-6.5e-15,-50.4) rot=(1,0,0;3.14159rad)
FEATURE [PartDesign::Body] Body427  label="Limb_Servohorn_Mount_long_v008"
  Group = -> [Sketch1731,Pad813,Sketch1712,SubtractivePipe016,Fillet239,Sketch1734,Pocket681,Sketch1720,Pocket685,Sketch1721,Pocket680,Fillet226,Sketch1727,Pocket673,Sketch1711,Pocket679,Fillet228]
  Origin = -> Origin599
  Tip = -> Fillet228
FEATURE [Part::Mirroring] Part__Mirroring009  label="Limb_Servohorn_Mount_long_v006 (Mirror #4)001"
  Base = (0,0,0)
  Normal = (0,0,1)
  Placement = pos=(0,0,-47.1) rot=(0,0,1;0rad)
  Source = -> Body427
FEATURE [PartDesign::Body] Body428  label="M2x065"
  Group = -> [Sketch1742,Pad793,Sketch1738,Pad807,Sketch1661,Pocket686,Chamfer319]
  Origin = -> Origin656
  Tip = -> Chamfer319
FEATURE [PartDesign::Body] Body429  label="red wire013"
  Group = -> [Sketch1651,Pad736]
  Origin = -> Origin675
  Placement = pos=(0,25.15,0) rot=(0,0,1;0rad)
  Tip = -> Pad736
FEATURE [PartDesign::Body] Body430  label="M3 Nut076"
  Group = -> [Sketch1749,Pad799,Sketch1819,Groove151,Chamfer326]
  Origin = -> Origin619
  Placement = pos=(-110.55,7.7,52.05) rot=(0.57735,0.57735,-0.57735;2.0944rad)
  Tip = -> Chamfer326
FEATURE [PartDesign::Body] Body431  label="Shoulder_Joint_Ball_Bearing_Pin006"
  Group = -> [Sketch1570,Pad711,Chamfer315]
  Origin = -> Origin614
  Placement = pos=(-115.146,-150.626,71.5546) rot=(-1,0,0;1.5708rad)
  Tip = -> Chamfer315
FEATURE [PartDesign::Body] Body432  label="M3 Nut077"
  Group = -> [Sketch1640,Pad789,Sketch1631,Groove165,Chamfer348]
  Origin = -> Origin716
  Placement = pos=(-23.1,-9.85,52.05) rot=(0.57735,-0.57735,0.57735;2.0944rad)
  Tip = -> Chamfer348
FEATURE [PartDesign::Body] Body433  label="Foot_Tip003"
  Group = -> [Sketch1599,Pad690,Sketch1589,Groove141,Sketch1682,SubtractivePipe018,PolarPattern003,Sketch1607,Groove143,Sketch1537,Pocket592,Sketch1610,Pocket590,Sketch1601,Pocket589,Sketch1605,Pocket626,Sketch1591,Pocket611,Sketch1617,Pocket607]
  Origin = -> Origin723
  Placement = pos=(0.75,0,37.62) rot=(0,1,0;3.14159rad)
  Tip = -> Pocket607
FEATURE [PartDesign::Body] Body434  label="M3x089"
  Group = -> [Sketch1650,Pad753,Sketch1792,Pad750,Sketch1803,Pocket582,Chamfer362]
  Origin = -> Origin606
  Placement = pos=(-71.5,-25.55,62.05) rot=(-1,0,0;1.5708rad)
  Tip = -> Chamfer362
FEATURE [PartDesign::Body] Body436  label="M2x066"
  Group = -> [Sketch1624,Pad693,Sketch1901,Pad699,Sketch1531,Pocket612,Chamfer381]
  Origin = -> Origin674
  Placement = pos=(-115.144,-143.75,71.585) rot=(1,0,0;1.5708rad)
  Tip = -> Chamfer381
FEATURE [App::Part] Part174  label="Ball Bearing Pin009"
  Group = -> [Body436,Body412,Body431]
  Origin = -> Origin584
  Placement = pos=(-247.6,-327.45,0) rot=(0,0,1;3.14159rad)
FEATURE [PartDesign::Body] Body437  label="M2 Nut059"
  Group = -> [Sketch1662,Pad812,Sketch1726,Groove168,Chamfer385,Sketch1730,Sketch1735]
  Origin = -> Origin596
  Placement = pos=(0,0,2.75) rot=(0,0,1;0rad)
  Tip = -> Chamfer385
FEATURE [App::Part] Part161  label="M050"
  Group = -> [Body428,Body437]
  Origin = -> Origin657
  Placement = pos=(-9.8e-15,-10.5,80) rot=(0,1,0;3.14159rad)
FEATURE [PartDesign::Body] Body438
  Group = -> [Sketch1825,Pad790,Sketch1745,Pocket701,Sketch1751,Pocket682,Sketch1748,Pocket698,Chamfer333]
  Origin = -> Origin691
  Tip = -> Chamfer333
FEATURE [PartDesign::Body] Body439  label="M3 Nut078"
  Group = -> [Sketch1539,Pad706,Sketch1594,Groove149,Chamfer328]
  Origin = -> Origin721
  Placement = pos=(-146.027,-159.25,78.1297) rot=(0.862856,-0.357407,0.357407;1.71777rad)
  Tip = -> Chamfer328
FEATURE [PartDesign::Body] Body440  label="Gear013"
  Group = -> [Sketch1644,Pad737,Sketch1645,Pocket572,Chamfer336]
  Origin = -> Origin618
  Placement = pos=(0,0,38.25) rot=(0,0,1;0rad)
  Tip = -> Chamfer336
FEATURE [PartDesign::Body] Body441  label="M3x090"
  Group = -> [Sketch1625,Pad710,Sketch1608,Pad717,Sketch1611,Pocket619,Chamfer375]
  Origin = -> Origin728
  Placement = pos=(0.72,13.88,34.3) rot=(1,0,0;1.5708rad)
  Tip = -> Chamfer375
FEATURE [PartDesign::Body] Body442  label="M3 Nut079"
  Group = -> [Sketch1566,Pad729,Sketch1604,Groove146,Chamfer309]
  Origin = -> Origin684
  Placement = pos=(-138.956,-159.25,84.9639) rot=(0.862856,-0.357407,0.357407;1.71777rad)
  Tip = -> Chamfer309
FEATURE [PartDesign::Body] Body444  label="M3x091"
  Group = -> [Sketch1804,Pad656,Sketch1784,Pad655,Sketch1797,Pocket565,Chamfer325]
  Origin = -> Origin603
  Placement = pos=(-115.35,28,62.05) rot=(1,0,0;1.5708rad)
  Tip = -> Chamfer325
FEATURE [PartDesign::Body] Body446  label="M3 Nut080"
  Group = -> [Sketch1626,Pad802,Sketch1622,Groove134,Chamfer373]
  Origin = -> Origin717
  Placement = pos=(-71.5,-9.8,62.05) rot=(0.57735,-0.57735,0.57735;2.0944rad)
  Tip = -> Chamfer373
FEATURE [PartDesign::Body] Body447  label="M3 Nut081"
  Group = -> [Sketch1820,Pad828,Sketch1639,Groove166,Chamfer324]
  Origin = -> Origin672
  Placement = pos=(-110.6,-9.3,52.1) rot=(0.57735,0.57735,-0.57735;2.0944rad)
  Tip = -> Chamfer324
FEATURE [PartDesign::Body] Body448  label="M3 Nut082"
  Group = -> [Sketch1534,Pad691,Sketch1545,Groove148,Chamfer305]
  Origin = -> Origin710
  Placement = pos=(-104.661,-159.25,50.9359) rot=(0.862856,-0.357407,0.357407;1.71777rad)
  Tip = -> Chamfer305
FEATURE [PartDesign::Body] Body449  label="MG996R011"
  Group = -> [Sketch1597,Pad715,Sketch1547,Pad798,Sketch1576,Pad791,Sketch1571,Pad800,Sketch1563,Pad721,Sketch1665,Pad826,Sketch1560,Pad730,Sketch1595,Pocket690,Sketch1541,Pocket624,Sketch1565,Pad827,Sketch1588,Pocket700,Fillet236,Sketch1568,Pad830,Sketch1580,Pad718,Sketch1554,Pad818,Chamfer306,Fillet211,Sketch1683,Pocket702]
  Origin = -> Origin615
  Tip = -> Pocket702
FEATURE [PartDesign::Body] Body450  label="M3 Nut083"
  Group = -> [Sketch1530,Pad697,Sketch1535,Groove145,Chamfer311]
  Origin = -> Origin737
  Placement = pos=(-111.697,-159.25,43.8385) rot=(0.862856,-0.357407,0.357407;1.71777rad)
  Tip = -> Chamfer311
FEATURE [App::Part] Part203  label="Lower Leg Counterpiece and Ball Bearing Pin003"
  Group = -> [Body414,Body450,Body448,Body439,Body442,Part__Mirroring008,Part174]
  Origin = -> Origin683
  Placement = pos=(49.45,155,49.5) rot=(0,0,1;0rad)
FEATURE [PartDesign::Body] Body451  label="brown wire012"
  Group = -> [Sketch1636,Pad796]
  Origin = -> Origin681
  Placement = pos=(0,25.15,0) rot=(0,0,1;0rad)
  Tip = -> Pad796
FEATURE [PartDesign::Body] Body452  label="M2 Nut061"
  Group = -> [Sketch1660,Pad811,Sketch1688,Groove167,Chamfer387,Sketch1558,Sketch1676]
  Origin = -> Origin626
  Placement = pos=(0,0,2.75) rot=(0,0,1;0rad)
  Tip = -> Chamfer387
FEATURE [App::Part] Part170  label="M055"
  Group = -> [Body416,Body452]
  Origin = -> Origin610
  Placement = pos=(9.1,-5.25,80) rot=(0,1,0;3.14159rad)
FEATURE [PartDesign::Body] Body453  label="M3x092"
  Group = -> [Sketch1785,Pad684,Sketch1788,Pad664,Sketch1796,Pocket635,Chamfer345]
  Origin = -> Origin732
  Placement = pos=(-23.1,-25.6,52) rot=(-1,0,0;1.5708rad)
  Tip = -> Chamfer345
FEATURE [PartDesign::Body] Body454  label="M2 Nut062"
  Group = -> [Sketch1732,Pad686,Sketch1717,Groove169,Chamfer363,Sketch1716,Sketch1713]
  Origin = -> Origin624
  Placement = pos=(0,0,2.75) rot=(0,0,1;0rad)
  Tip = -> Chamfer363
FEATURE [PartDesign::Body] Body455  label="M3x093"
  Group = -> [Sketch1653,Pad653,Sketch1658,Pad756,Sketch1643,Pocket573,Chamfer351]
  Origin = -> Origin696
  Placement = pos=(-115.35,-29.35,62.05) rot=(-1,0,0;1.5708rad)
  Tip = -> Chamfer351
FEATURE [PartDesign::Body] Body456  label="brown wire013"
  Group = -> [Sketch1569,Pad820]
  Origin = -> Origin622
  Placement = pos=(0,25.15,0) rot=(0,0,1;0rad)
  Tip = -> Pad820
FEATURE [PartDesign::Body] Body457  label="orange wire012"
  Group = -> [Sketch1646,Pad751]
  Origin = -> Origin702
  Placement = pos=(0,25.15,0) rot=(0,0,1;0rad)
  Tip = -> Pad751
FEATURE [PartDesign::Body] Body458
  Origin = -> Origin722
FEATURE [PartDesign::Body] Body459  label="MG996R012"
  Group = -> [Sketch1642,Pad794,Sketch1752,Pad745,Sketch1623,Pad792,Sketch1656,Pad747,Sketch1620,Pad659,Sketch1630,Pad748,Sketch1635,Pad806,Sketch1649,Pocket574,Sketch1634,Pocket628,Sketch1627,Pad752,Sketch1648,Pocket575,Fillet210,Sketch1654,Pad795,Sketch1615,Pad652,Sketch1633,Pad755,Chamfer374,Fillet218,Sketch1641,Pocket629]
  Origin = -> Origin695
  Tip = -> Pocket629
FEATURE [App::Part] Part188  label="Servo011"
  Group = -> [Body459,Body440,Body429,Body457,Body451]
  Origin = -> Origin704
  Placement = pos=(-47.3841,-8.5,56.9914) rot=(-0.57735,-0.57735,-0.57735;2.0944rad)
FEATURE [PartDesign::Body] Body460  label="M2x067"
  Group = -> [Sketch1733,Pad695,Sketch1729,Pad810,Sketch1740,Pocket687,Chamfer384]
  Origin = -> Origin582
  Tip = -> Chamfer384
FEATURE [App::Part] Part176  label="M057"
  Group = -> [Body460,Body454]
  Origin = -> Origin617
  Placement = pos=(-9.8e-15,10.5,80) rot=(0,1,0;3.14159rad)
FEATURE [PartDesign::Body] Body461  label="M3x094"
  Group = -> [Sketch1577,Pad708,Sketch1686,Pad696,Sketch1664,Pocket602,Chamfer304]
  Origin = -> Origin676
  Placement = pos=(-149,-30,75) rot=(-1,0,0;1.5708rad)
  Tip = -> Chamfer304
FEATURE [PartDesign::Body] Body462  label="M3 Nut084"
  Group = -> [Sketch1637,Pad809,Sketch1628,Groove153,Chamfer346]
  Origin = -> Origin621
  Placement = pos=(-23,-9.8,62.05) rot=(0.57735,-0.57735,0.57735;2.0944rad)
  Tip = -> Chamfer346
FEATURE [PartDesign::Body] Body463  label="M3x095"
  Group = -> [Sketch1904,Pad716,Sketch1613,Pad705,Sketch1609,Pocket616,Chamfer372]
  Origin = -> Origin707
  Placement = pos=(0.75,-14,34.25) rot=(-1,0,0;1.5708rad)
  Tip = -> Chamfer372
FEATURE [App::Part] Part201  label="Screws013"
  Group = -> [Body463,Body441]
  Origin = -> Origin706
FEATURE [PartDesign::Body] Body464
  Group = -> [Sketch1744,Pad829,Chamfer341]
  Origin = -> Origin634
  Tip = -> Chamfer341
FEATURE [App::Part] Part205  label="Ball Bearing003"
  Group = -> [Body438,Body464,Body458]
  Origin = -> Origin664
  Placement = pos=(-144.1,-23.5,26.95) rot=(1,0,0;1.5708rad)
FEATURE [PartDesign::Body] Body465  label="M3 Nut085"
  Group = -> [Sketch1747,Pad801,Sketch1757,Groove152,Chamfer371]
  Origin = -> Origin715
  Placement = pos=(-71.6,-9.85,52.05) rot=(0.57735,-0.57735,0.57735;2.0944rad)
  Tip = -> Chamfer371
FEATURE [App::Part] Part200  label="Servo Nuts003"
  Group = -> [Body446,Body462,Body465,Body432]
  Origin = -> Origin693
  Placement = pos=(0,17.9,0) rot=(0,0,1;0rad)
FEATURE [PartDesign::Body] Body466  label="M3x096"
  Group = -> [Sketch1652,Pad742,Sketch1657,Pad663,Sketch1801,Pocket570,Chamfer349]
  Origin = -> Origin629
  Placement = pos=(-110.55,28,52.05) rot=(1,0,0;1.5708rad)
  Tip = -> Chamfer349
FEATURE [App::Part] Part187  label="Shell Screws003"
  Group = -> [Body455,Body423,Body444,Body466]
  Origin = -> Origin609
FEATURE [PartDesign::Body] Body468  label="M3x097"
  Group = -> [Sketch1638,Pad749,Sketch1791,Pad675,Sketch1647,Pocket567,Chamfer353]
  Origin = -> Origin668
  Placement = pos=(-71.6,-25.55,52.05) rot=(-1,0,0;1.5708rad)
  Tip = -> Chamfer353
FEATURE [PartDesign::Body] Body471  label="Rubber Dampener037"
  Group = -> [Sketch1866,Revolution036,Fillet215]
  Origin = -> Origin713
  Placement = pos=(-55.25,-12.25,100.75) rot=(-1,0,0;1.5708rad)
  Tip = -> Fillet215
FEATURE [PartDesign::Body] Body473  label="Rubber Dampener038"
  Group = -> [Sketch1761,Revolution043,Fillet232]
  Origin = -> Origin644
  Placement = pos=(-55.25,-12.25,100.75) rot=(-1,0,0;1.5708rad)
  Tip = -> Fillet232
FEATURE [PartDesign::Body] Body475  label="M3 Nut086"
  Group = -> [Sketch1602,Pad688,Sketch1612,Groove147,Chamfer342]
  Origin = -> Origin735
  Placement = pos=(0.75,-5.5,34.25) rot=(1,0,0;1.5708rad)
  Tip = -> Chamfer342
FEATURE [App::Part] Part186  label="Nuts003"
  Group = -> [Body475,Body415]
  Origin = -> Origin720
FEATURE [PartDesign::Body] Body476  label="Limb_Ball_Bearing_Mount_long_v007"
  Group = -> [Sketch1556,Pad814,Sketch1553,SubtractivePipe020,Fillet194,Sketch1684,Pocket604,Sketch1542,Pocket615,Sketch1550,Pocket600,Sketch1544,Pocket676,Fillet227,Fillet205]
  Origin = -> Origin690
  Tip = -> Fillet205
FEATURE [Part::Mirroring] Part__Mirroring011  label="Limb_Ball_Bearing_Mount_long_v005 (Mirror #5)001"
  Base = (0,0,0)
  Normal = (0,0,1)
  Placement = pos=(0,0,-47.15) rot=(0,0,1;0rad)
  Source = -> Body476
FEATURE [App::Part] Part171  label="ball bearing moung003"
  Group = -> [Body476,Part__Mirroring011]
  Origin = -> Origin694
  Placement = pos=(-144.1,22.7,27.05) rot=(0,0.707107,0.707107;3.14159rad)
FEATURE [PartDesign::Body] Body477  label="Wrist003"
  Group = -> [Sketch1585,Pad698,Sketch1596,Pocket614,Fillet206,Sketch1689,Pocket596,Pad709,Sketch1603,Pocket599,Sketch1593,Pocket593,Fillet233,Sketch1584,Pocket591,Sketch1606,Pocket597,Sketch1592,Sketch1598,Pocket594,Pocket610,Chamfer339,Sketch1579,Pocket608,Fillet208]
  Origin = -> Origin731
  Placement = pos=(-66.468,-10,83.4386) rot=(0.281085,0.678598,0.678598;3.68962rad)
  Tip = -> Fillet208
FEATURE [Part::Mirroring] Part__Mirroring012  label="Wrist001 (Mirror #2)001"
  Base = (0,0,0)
  Normal = (0,0,1)
  Placement = pos=(0,0,0) rot=(1,0,0;3.14159rad)
  Source = -> Body477
FEATURE [App::Part] Part181  label="Lower Leg and foot003"
  Group = -> [Body477,Body433,Part__Mirroring012]
  Origin = -> Origin687
FEATURE [PartDesign::Body] Body479  label="Rubber Dampener039"
  Group = -> [Sketch1762,Revolution039,Fillet225]
  Origin = -> Origin678
  Placement = pos=(-96.5,-12.25,127.7) rot=(-1,0,0;1.5708rad)
  Tip = -> Fillet225
FEATURE [PartDesign::Body] Body490  label="Rubber Dampener040"
  Group = -> [Sketch1869,Revolution046,Fillet217]
  Origin = -> Origin649
  Placement = pos=(-96.5,-12.25,127.7) rot=(-1,0,0;1.5708rad)
  Tip = -> Fillet217
FEATURE [PartDesign::Body] Body492  label="Rubber Dampener041"
  Group = -> [Sketch1718,Revolution047,Fillet222]
  Origin = -> Origin736
  Placement = pos=(-62.3,-12.25,93.7) rot=(-1,0,0;1.5708rad)
  Tip = -> Fillet222
FEATURE [PartDesign::Body] Body497  label="Rubber Dampener042"
  Group = -> [Sketch1864,Revolution038,Fillet209]
  Origin = -> Origin688
  Placement = pos=(-62.3,-12.25,93.7) rot=(-1,0,0;1.5708rad)
  Tip = -> Fillet209
FEATURE [PartDesign::Body] Body501  label="M3x104"
  Group = -> [Sketch1786,Pad658,Sketch1655,Pad668,Sketch1787,Pocket569,Chamfer356]
  Origin = -> Origin590
  Placement = pos=(-23,-25.6,62.05) rot=(-1,0,0;1.5708rad)
  Tip = -> Chamfer356
FEATURE [App::Part] Part175  label="Servo Screws003"
  Group = -> [Body434,Body468,Body501,Body453]
  Origin = -> Origin669
  Placement = pos=(0,1.4e-14,114.1) rot=(1,0,0;3.14159rad)
FEATURE [PartDesign::Body] Body504  label="M3x105"
  Group = -> [Sketch1680,Pad700,Sketch1578,Pad731,Sketch1674,Pocket623,Chamfer307]
  Origin = -> Origin705
  Placement = pos=(-121.75,-30,34) rot=(-1,0,0;1.5708rad)
  Tip = -> Chamfer307
FEATURE [PartDesign::Body] Body507  label="M2x073"
  Group = -> [Sketch1671,Pad687,Sketch1669,Pad815,Sketch1679,Pocket683,Chamfer322]
  Origin = -> Origin611
  Tip = -> Chamfer322
FEATURE [App::Part] Part168  label="M053"
  Group = -> [Body507,Body425]
  Origin = -> Origin641
  Placement = pos=(9.1,5.25,80) rot=(0,1,0;3.14159rad)
FEATURE [App::Part] Part164  label="Screws011"
  Group = -> [Part176,Part161,Part165,Part170,Part168,Part194]
  Origin = -> Origin605
  Placement = pos=(0,1.16e-14,23.75) rot=(1,0,0;3.14159rad)
FEATURE [App::Part] Part160  label="servohorn moun tpost003"
  Group = -> [Body427,Part180,Part164,Part__Mirroring009]
  Origin = -> Origin580
  Placement = pos=(-144.1,-24.45,27.05) rot=(1,0,0;1.5708rad)
FEATURE [PartDesign::Body] Body508  label="Rubber Dampener043"
  Group = -> [Sketch1766,Revolution044,Fillet229]
  Origin = -> Origin670
  Placement = pos=(-89.5,-12.25,134.7) rot=(-1,0,0;1.5708rad)
  Tip = -> Fillet229
FEATURE [App::Part] Part195  label="Rubber Dampeners009"
  Group = -> [Body508,Body490,Body473,Body492]
  Origin = -> Origin667
  Placement = pos=(0,24.35,0) rot=(0,0,1;0rad)
FEATURE [PartDesign::Body] Body510  label="Rubber Dampener045"
  Group = -> [Sketch1871,Revolution042,Fillet202]
  Origin = -> Origin724
  Placement = pos=(-89.5,-12.25,134.7) rot=(-1,0,0;1.5708rad)
  Tip = -> Fillet202
FEATURE [App::Part] Part204  label="Rubber Dampeners011"
  Group = -> [Body510,Body479,Body471,Body497]
  Origin = -> Origin730
  Placement = pos=(87.2923,32.35,29.8753) rot=(0,1,0;5.49779rad)
FEATURE [PartDesign::Body] Body512  label="Limb_Bottom_Shell003"
  Group = -> [Sketch1564,Pad824,Pocket703,Pocket663,Sketch1811,SubtractivePipe017,Fillet197,Sketch1824,Pocket664,Sketch1533,Pocket695,Sketch1816,Pocket704,Pad819,Fillet193,Sketch1812,Pocket688,Fillet213,Sketch1587,Pocket659,Sketch1549,Pocket694,Sketch1818,Pocket669,Sketch1540,Pocket693,Sketch1581,Pocket689,Sketch1809,Pocket625,Sketch1817,Pocket691,Sketch1532,Pocket692,Sketch1548,Pocket605,Sketch1546,Pocket677,+5 more]
  Origin = -> Origin719
  Placement = pos=(-144.05,-29.45,42.05) rot=(0,0,1;0rad)
  Tip = -> Fillet198
FEATURE [Part::Mirroring] Part__Mirroring013  label="Limb_Bottom_Shell001 (Mirror #7)001"
  Base = (0,0,0)
  Normal = (0,0,1)
  Placement = pos=(0,-1.9,0) rot=(1,0,0;3.14159rad)
  Source = -> Body512
FEATURE [PartDesign::Body] Body516  label="orange wire014"
  Group = -> [Sketch1552,Pad703]
  Origin = -> Origin663
  Placement = pos=(0,25.15,0) rot=(0,0,1;0rad)
  Tip = -> Pad703
FEATURE [App::Part] Part190  label="Servo012"
  Group = -> [Body449,Body421,Body420,Body516,Body456]
  Origin = -> Origin729
  Placement = pos=(-75.5841,-15.9,113.841) rot=(0.281085,-0.678598,-0.678598;3.68962rad)
FEATURE [PartDesign::Body] Body517  label="M3x108"
  Group = -> [Sketch1572,Pad713,Sketch1582,Pad722,Sketch1586,Pocket622,Chamfer313]
  Origin = -> Origin601
  Placement = pos=(-156,-30,68) rot=(-1,0,0;1.5708rad)
  Tip = -> Chamfer313
FEATURE [PartDesign::Body] Body519  label="M3x109"
  Group = -> [Sketch1798,Pad671,Sketch1790,Pad660,Sketch1783,Pocket568,Chamfer367]
  Origin = -> Origin685
  Placement = pos=(-144.1,30.35,27.05) rot=(0,0.707107,-0.707107;3.14159rad)
  Tip = -> Chamfer367
FEATURE [PartDesign::Body] Body524  label="M3 Nut094"
  Group = -> [Sketch1629,Pad654,Sketch1619,Groove136,Chamfer352]
  Origin = -> Origin662
  Placement = pos=(-115.35,-9.3,62.1) rot=(0.57735,0.57735,-0.57735;2.0944rad)
  Tip = -> Chamfer352
FEATURE [App::Part] Part191  label="Shell Nuts003"
  Group = -> [Body424,Body430,Body524,Body447]
  Origin = -> Origin689
FEATURE [App::Part] Part189  label="FR Upper Leg001"
  Group = -> [Part160,Part171,Body413,Body512,Part191,Part200,Part205,Part188,Part187,Part175,Body519,Part204,Part__Mirroring014,Part__Mirroring013]
  Origin = -> Origin665
  Placement = pos=(55.5497,1.35,169.885) rot=(0,1,0;5.75959rad)
FEATURE [PartDesign::Body] Body527  label="M3x111"
  Group = -> [Sketch1574,Pad728,Sketch1551,Pad701,Sketch1573,Pocket621,Chamfer312]
  Origin = -> Origin638
  Placement = pos=(-114.75,-30,41) rot=(-1,0,0;1.5708rad)
  Tip = -> Chamfer312
FEATURE [App::Part] Part192  label="m3x20 screws003"
  Group = -> [Body461,Body517,Body504,Body527]
  Origin = -> Origin581
  Placement = pos=(-21.55,-12.1,-20.7) rot=(-0.707107,0,0.707107;3.14159rad)
FEATURE [App::Part] Part199  label="FR Lower Leg001"
  Group = -> [Part186,Part201,Part181,Part203,Part192,Part190,Part195]
  Origin = -> Origin726
  Placement = pos=(-0.0178536,-0.3,0.205627) rot=(0,0,1;0rad)
FEATURE [Sketcher::SketchObject] Sketch1905
  MapMode = 5
  Support = -> [XY_Plane773]
  sketch-geometry (2):
    g0: Circle CenterX=0 CenterY=0 CenterZ=0 NormalX=0 NormalY=0 NormalZ=1 AngleXU=0 Radius=2.5
    g1: Circle CenterX=0 CenterY=0 CenterZ=0 NormalX=0 NormalY=0 NormalZ=1 AngleXU=0 Radius=1
  constraints (4):
    c: Coincident(g0,g-1)
    c: Coincident(g1,g0)
    c: Radius(g0) = 2.5
    c: Radius(g1) = 1
FEATURE [Sketcher::SketchObject] Sketch1906
  MapMode = 5
  Support = -> [XY_Plane767]
FEATURE [Sketcher::SketchObject] Sketch1907
  MapMode = 5
  Support = -> [XY_Plane767]
FEATURE [Sketcher::SketchObject] Sketch1909
  MapMode = 5
  Support = -> [XY_Plane770]
  sketch-geometry (8):
    g0: LineSegment StartX=0 StartY=2.3094 StartZ=0 EndX=-2 EndY=1.1547 EndZ=0
    g1: LineSegment StartX=-2 StartY=1.1547 StartZ=0 EndX=-2 EndY=-1.1547 EndZ=0
    g2: LineSegment StartX=-2 StartY=-1.1547 StartZ=0 EndX=-2e-16 EndY=-2.3094 EndZ=0
    g3: LineSegment StartX=-2e-16 StartY=-2.3094 StartZ=0 EndX=2 EndY=-1.1547 EndZ=0
    g4: LineSegment StartX=2 StartY=-1.1547 StartZ=0 EndX=2 EndY=1.1547 EndZ=0
    g5: LineSegment StartX=2 StartY=1.1547 StartZ=0 EndX=0 EndY=2.3094 EndZ=0
    g6: Circle [constr] CenterX=0 CenterY=0 CenterZ=0 NormalX=0 NormalY=0 NormalZ=1 AngleXU=0 Radius=2.3094
    g7: Circle CenterX=0 CenterY=0 CenterZ=0 NormalX=0 NormalY=0 NormalZ=1 AngleXU=0 Radius=1
  constraints (18):
    c: Coincident(g0,g1)
    c: Coincident(g1,g2)
    c: Coincident(g2,g3)
    c: Coincident(g3,g4)
    c: Coincident(g4,g5)
    c: Coincident(g5,g0)
    c: Equal(g0, g1-g5) x5
    c: PointOnObject(g0,g6)
    c: PointOnObject(g1,g6)
    c: PointOnObject(g2,g6)
    c: PointOnObject(g3,g6)
    c: PointOnObject(g4,g6)
    c: PointOnObject(g5,g6)
    c: Coincident(g6,g-1)
    c: PointOnObject(g5,g-2)
    c: DistanceX(g0,g4) = 4
    c: Coincident(g7,g-1)
    c: Radius(g7) = 1
FEATURE [PartDesign::Pad] Pad838  label="Ball Bearing Pin010"
  Length = 5
  Length2 = 100
  Profile = -> Sketch1905
  Type = 0
FEATURE [PartDesign::Chamfer] Chamfer391  label="Smooth Pinhead007"
  Base = -> Pad838 [Edge3]
  BaseFeature = -> Pad838
  Size = 0.4
FEATURE [PartDesign::Pad] Pad848  label="M3 Nut Primitive167"
  Length = 0.6
  Length2 = 0.6
  Profile = -> Sketch1909
  Type = 4
FEATURE [PartDesign::Body] Body545  label="Shoulder_Joint_Ball_Bearing_Pin007"
  Group = -> [Sketch1905,Pad838,Chamfer391]
  Origin = -> Origin764
  Placement = pos=(-21.75,10,15) rot=(0,-1,0;1.5708rad)
  Tip = -> Chamfer391
FEATURE [Sketcher::SketchObject] Sketch1915
  MapMode = 5
  Support = -> [XY_Plane744]
  sketch-geometry (13):
    g0: Circle [constr] CenterX=0 CenterY=0 CenterZ=0 NormalX=0 NormalY=0 NormalZ=1 AngleXU=0 Radius=20
    g1: LineSegment [constr] StartX=-14.1421 StartY=14.1421 StartZ=0 EndX=14.1421 EndY=14.1421 EndZ=0
    g2: LineSegment [constr] StartX=14.1421 StartY=14.1421 StartZ=0 EndX=14.1421 EndY=-14.1421 EndZ=0
    g3: LineSegment [constr] StartX=14.1421 StartY=-14.1421 StartZ=0 EndX=-14.1421 EndY=-14.1421 EndZ=0
    g4: LineSegment [constr] StartX=-14.1421 StartY=-14.1421 StartZ=0 EndX=-14.1421 EndY=14.1421 EndZ=0
    g5: ArcOfCircle CenterX=0 CenterY=0 CenterZ=0 NormalX=0 NormalY=0 NormalZ=1 AngleXU=0 Radius=20 StartAngle=2.60685 EndAngle=3.67634
    g6: ArcOfCircle CenterX=-14.1421 CenterY=14.1421 CenterZ=0 NormalX=0 NormalY=0 NormalZ=1 AngleXU=0 Radius=5 StartAngle=0.66007 EndAngle=4.05232
    g7: ArcOfCircle CenterX=14.1421 CenterY=14.1421 CenterZ=0 NormalX=0 NormalY=0 NormalZ=1 AngleXU=0 Radius=5 StartAngle=5.37246 EndAngle=8.76471
    g8: ArcOfCircle CenterX=14.1421 CenterY=-14.1421 CenterZ=0 NormalX=0 NormalY=0 NormalZ=1 AngleXU=0 Radius=5 StartAngle=3.80166 EndAngle=7.19391
    g9: ArcOfCircle CenterX=-14.1421 CenterY=-14.1421 CenterZ=0 NormalX=0 NormalY=0 NormalZ=1 AngleXU=0 Radius=5 StartAngle=2.23087 EndAngle=5.62311
    g10: ArcOfCircle CenterX=0 CenterY=0 CenterZ=0 NormalX=0 NormalY=0 NormalZ=1 AngleXU=0 Radius=20 StartAngle=1.03605 EndAngle=2.10554
    g11: ArcOfCircle CenterX=0 CenterY=0 CenterZ=0 NormalX=0 NormalY=0 NormalZ=1 AngleXU=0 Radius=20 StartAngle=5.74844 EndAngle=6.81793
    g12: ArcOfCircle CenterX=0 CenterY=0 CenterZ=0 NormalX=0 NormalY=0 NormalZ=1 AngleXU=0 Radius=20 StartAngle=4.17765 EndAngle=5.24713
  constraints (38):
    c: Coincident(g0,g-1)
    c: Radius(g0) = 20
    c: Coincident(g1,g2)
    c: Coincident(g2,g3)
    c: Coincident(g3,g4)
    c: Coincident(g4,g1)
    c: Horizontal(g1)
    c: Horizontal(g3)
    c: Vertical(g2)
    c: Vertical(g4)
    c: PointOnObject(g1,g0)
    c: PointOnObject(g2,g0)
    c: Equal(g1,g2)
    c: PointOnObject(g1,g0)
    c: Coincident(g5,g-1)
    c: Radius(g5) = 20
    c: Coincident(g6,g1)
    c: Coincident(g7,g1)
    c: Coincident(g8,g2)
    c: Coincident(g9,g3)
    c: Coincident(g5,g6)
    c: Equal(g5,g10)
    c: Coincident(g10,g7)
    c: Coincident(g5,g10)
    c: Coincident(g11,g7)
    c: Equal(g5,g11)
    c: Coincident(g11,g8)
    c: Coincident(g5,g11)
    c: Coincident(g12,g8)
    c: Equal(g5,g12)
    c: Coincident(g12,g9)
    c: Coincident(g5,g12)
    c: Coincident(g5,g9)
    c: Coincident(g6,g10)
    c: Radius(g6) = 5
    c: Equal(g6,g7)
    c: Equal(g6,g8)
    c: Equal(g6,g9)
FEATURE [PartDesign::Pad] Pad867  label="Baseplate038"
  Length = 12
  Length2 = 100
  Profile = -> Sketch1915
  Type = 0
FEATURE [Sketcher::SketchObject] Sketch1922
  MapMode = 5
  Support = -> [XY_Plane769]
  sketch-geometry (8):
    g0: LineSegment StartX=-16.75 StartY=28.25 StartZ=0 EndX=16.75 EndY=28.25 EndZ=0
    g1: LineSegment StartX=21.75 StartY=23.25 StartZ=0 EndX=21.75 EndY=-23.25 EndZ=0
    g2: LineSegment StartX=16.75 StartY=-28.25 StartZ=0 EndX=-16.75 EndY=-28.25 EndZ=0
    g3: LineSegment StartX=-21.75 StartY=-23.25 StartZ=0 EndX=-21.75 EndY=23.25 EndZ=0
    g4: ArcOfCircle CenterX=-16.75 CenterY=23.25 CenterZ=0 NormalX=0 NormalY=0 NormalZ=1 AngleXU=0 Radius=5 StartAngle=1.5708 EndAngle=3.14159
    g5: ArcOfCircle CenterX=16.75 CenterY=23.25 CenterZ=0 NormalX=0 NormalY=0 NormalZ=1 AngleXU=0 Radius=5 StartAngle=1e-16 EndAngle=1.5708
    g6: ArcOfCircle CenterX=16.75 CenterY=-23.25 CenterZ=0 NormalX=0 NormalY=0 NormalZ=1 AngleXU=0 Radius=5 StartAngle=4.71239 EndAngle=6.28319
    g7: ArcOfCircle CenterX=-16.75 CenterY=-23.25 CenterZ=0 NormalX=0 NormalY=0 NormalZ=1 AngleXU=0 Radius=5 StartAngle=3.14159 EndAngle=4.71239
  constraints (18):
    c: Horizontal(g2)
    c: Vertical(g1)
    c: Tangent(g3,g4) = 1.5708
    c: Tangent(g0,g4) = 1.5708
    c: Tangent(g0,g5) = 1.5708
    c: Tangent(g1,g5) = 1.5708
    c: Tangent(g1,g6) = 1.5708
    c: Tangent(g2,g6) = 1.5708
    c: Tangent(g2,g7) = 1.5708
    c: Tangent(g3,g7) = 1.5708
    c: Equal(g4,g5)
    c: Equal(g5,g7)
    c: Equal(g7,g6)
    c: Radius(g5) = 5
    c: DistanceY(g2,g0) = 56.5
    c: DistanceX(g3,g1) = 43.5
    c: Symmetric(g0,g0,g-2)
    c: Symmetric(g3,g3,g-1)
FEATURE [PartDesign::Pad] Pad866  label="Baseplate037"
  Length = 5
  Length2 = 100
  Profile = -> Sketch1922
  Type = 0
FEATURE [PartDesign::Pad] Pad861  label="Baseplate Expansion003"
  BaseFeature = -> Pad866
  Length = 20
  Length2 = 100
  Profile = -> Pad866 [Face10]
  Type = 0
FEATURE [Sketcher::SketchObject] Sketch1918
  MapMode = 5
  Placement = pos=(0,0,25) rot=(0,0,1;0rad)
  Support = -> [Pad861]
  sketch-geometry (8):
    g0: LineSegment StartX=9.75 StartY=28.25 StartZ=0 EndX=9.75 EndY=20.25 EndZ=0
    g1: LineSegment StartX=9.75 StartY=20.25 StartZ=0 EndX=-18.75 EndY=20.25 EndZ=0
    g2: LineSegment StartX=-18.75 StartY=20.25 StartZ=0 EndX=-18.75 EndY=-20.25 EndZ=0
    g3: LineSegment StartX=-18.75 StartY=-20.25 StartZ=0 EndX=9.75 EndY=-20.25 EndZ=0
    g4: LineSegment StartX=9.75 StartY=-20.25 StartZ=0 EndX=9.75 EndY=-28.25 EndZ=0
    g5: LineSegment StartX=9.75 StartY=-28.25 StartZ=0 EndX=21.75 EndY=-28.25 EndZ=0
    g6: LineSegment StartX=21.75 StartY=-28.25 StartZ=0 EndX=21.75 EndY=28.25 EndZ=0
    g7: LineSegment StartX=21.75 StartY=28.25 StartZ=0 EndX=9.75 EndY=28.25 EndZ=0
  constraints (22):
    c: Vertical(g0)
    c: Coincident(g0,g1)
    c: Horizontal(g1)
    c: Coincident(g1,g2)
    c: Coincident(g2,g3)
    c: Horizontal(g3)
    c: Coincident(g3,g4)
    c: Vertical(g4)
    c: Coincident(g4,g5)
    c: Horizontal(g5)
    c: Coincident(g5,g6)
    c: Coincident(g6,g7)
    c: Coincident(g7,g0)
    c: Horizontal(g7)
    c: Equal(g7,g5)
    c: Symmetric(g6,g5,g-1)
    c: Symmetric(g1,g2,g-1)
    c: DistanceY(g6,g6) = 56.5
    c: DistanceX(g-1,g6) = 21.75
    c: DistanceX(g1,g-1) = 18.75
    c: DistanceY(g0,g0) = 8
    c: DistanceX(g1,g0) = 28.5
FEATURE [PartDesign::Pocket] Pocket723  label="Servo Pocket014"
  BaseFeature = -> Pad861
  Length = 20
  Length2 = 100
  Profile = -> Sketch1918
  Type = 0
FEATURE [Sketcher::SketchObject] Sketch1919
  MapMode = 5
  Placement = pos=(0,0,5) rot=(0,0,1;0rad)
  Support = -> [Pocket723]
  sketch-geometry (1):
    g0: Circle CenterX=0 CenterY=0 CenterZ=0 NormalX=0 NormalY=0 NormalZ=1 AngleXU=0 Radius=16.5
  constraints (2):
    c: Coincident(g0,g-1)
    c: Radius(g0) = 16.5
FEATURE [PartDesign::Pocket] Pocket719  label="Accesshole Servohorn Cap003"
  BaseFeature = -> Pocket723
  Length = 5
  Length2 = 100
  Profile = -> Sketch1919
  Type = 0
FEATURE [Sketcher::SketchObject] Sketch1917
  MapMode = 5
  Placement = pos=(0,0,5) rot=(0,0,1;0rad)
  Support = -> [Pocket719]
  sketch-geometry (9):
    g0: Circle [constr] CenterX=0 CenterY=0 CenterZ=0 NormalX=0 NormalY=0 NormalZ=1 AngleXU=0 Radius=20
    g1: LineSegment [constr] StartX=-14.1421 StartY=14.1421 StartZ=0 EndX=14.1421 EndY=14.1421 EndZ=0
    g2: LineSegment [constr] StartX=14.1421 StartY=14.1421 StartZ=0 EndX=14.1421 EndY=-14.1421 EndZ=0
    g3: LineSegment [constr] StartX=14.1421 StartY=-14.1421 StartZ=0 EndX=-14.1421 EndY=-14.1421 EndZ=0
    g4: LineSegment [constr] StartX=-14.1421 StartY=-14.1421 StartZ=0 EndX=-14.1421 EndY=14.1421 EndZ=0
    g5: Circle CenterX=-14.1421 CenterY=14.1421 CenterZ=0 NormalX=0 NormalY=0 NormalZ=1 AngleXU=0 Radius=1.6
    g6: Circle CenterX=14.1421 CenterY=14.1421 CenterZ=0 NormalX=0 NormalY=0 NormalZ=1 AngleXU=0 Radius=1.6
    g7: Circle CenterX=14.1421 CenterY=-14.1421 CenterZ=0 NormalX=0 NormalY=0 NormalZ=1 AngleXU=0 Radius=1.6
    g8: Circle CenterX=-14.1421 CenterY=-14.1421 CenterZ=0 NormalX=0 NormalY=0 NormalZ=1 AngleXU=0 Radius=1.6
  constraints (22):
    c: Coincident(g0,g-1)
    c: Radius(g0) = 20
    c: Coincident(g1,g2)
    c: Coincident(g2,g3)
    c: Coincident(g3,g4)
    c: Coincident(g4,g1)
    c: Horizontal(g1)
    c: Horizontal(g3)
    c: Vertical(g2)
    c: Vertical(g4)
    c: PointOnObject(g1,g0)
    c: PointOnObject(g2,g0)
    c: PointOnObject(g1,g0)
    c: Equal(g1,g2)
    c: Coincident(g5,g1)
    c: Coincident(g6,g1)
    c: Coincident(g7,g2)
    c: Coincident(g8,g3)
    c: Radius(g5) = 1.6
    c: Equal(g5,g6)
    c: Equal(g5,g7)
    c: Equal(g5,g8)
FEATURE [PartDesign::Pocket] Pocket707  label="Screwholes Servohorn Cap003"
  BaseFeature = -> Pocket719
  Length = 5
  Length2 = 100
  Profile = -> Sketch1917
  Type = 0
FEATURE [Sketcher::SketchObject] Sketch1923
  MapMode = 5
  Placement = pos=(0,0,5) rot=(0,0,1;0rad)
  Support = -> [Pocket707]
  sketch-geometry (35):
    g0: Circle [constr] CenterX=0 CenterY=0 CenterZ=0 NormalX=0 NormalY=0 NormalZ=1 AngleXU=0 Radius=20
    g1: LineSegment [constr] StartX=-14.1421 StartY=14.1421 StartZ=0 EndX=14.1421 EndY=-14.1421 EndZ=0
    g2: LineSegment [constr] StartX=14.1421 StartY=14.1421 StartZ=0 EndX=-14.1421 EndY=-14.1421 EndZ=0
    g3: LineSegment [constr] StartX=-14.1421 StartY=14.1421 StartZ=0 EndX=14.1421 EndY=14.1421 EndZ=0
    g4: LineSegment [constr] StartX=14.1421 StartY=14.1421 StartZ=0 EndX=14.1421 EndY=-14.1421 EndZ=0
    g5: LineSegment [constr] StartX=14.1421 StartY=-14.1421 StartZ=0 EndX=-14.1421 EndY=-14.1421 EndZ=0
    g6: LineSegment [constr] StartX=-14.1421 StartY=-14.1421 StartZ=0 EndX=-14.1421 EndY=14.1421 EndZ=0
    g7: LineSegment StartX=-11.8151 StartY=16.4692 StartZ=0 EndX=-14.9939 EndY=17.3209 EndZ=0
    g8: LineSegment StartX=-14.9939 StartY=17.3209 StartZ=0 EndX=-17.3209 EndY=14.9939 EndZ=0
    g9: LineSegment StartX=-17.3209 StartY=14.9939 StartZ=0 EndX=-16.4692 EndY=11.8151 EndZ=0
    g10: LineSegment StartX=-16.4692 StartY=11.8151 StartZ=0 EndX=-13.2904 EndY=10.9634 EndZ=0
    g11: LineSegment StartX=-13.2904 StartY=10.9634 StartZ=0 EndX=-10.9634 EndY=13.2904 EndZ=0
    g12: LineSegment StartX=-10.9634 StartY=13.2904 StartZ=0 EndX=-11.8151 EndY=16.4692 EndZ=0
    g13: Circle [constr] CenterX=-14.1421 CenterY=14.1421 CenterZ=0 NormalX=0 NormalY=0 NormalZ=1 AngleXU=0 Radius=3.2909
    g14: LineSegment StartX=14.9939 StartY=17.3209 StartZ=0 EndX=11.8151 EndY=16.4692 EndZ=0
    g15: LineSegment StartX=11.8151 StartY=16.4692 StartZ=0 EndX=10.9634 EndY=13.2904 EndZ=0
    g16: LineSegment StartX=10.9634 StartY=13.2904 StartZ=0 EndX=13.2904 EndY=10.9634 EndZ=0
    g17: LineSegment StartX=13.2904 StartY=10.9634 StartZ=0 EndX=16.4692 EndY=11.8151 EndZ=0
    g18: LineSegment StartX=16.4692 StartY=11.8151 StartZ=0 EndX=17.3209 EndY=14.9939 EndZ=0
    g19: LineSegment StartX=17.3209 StartY=14.9939 StartZ=0 EndX=14.9939 EndY=17.3209 EndZ=0
    g20: Circle [constr] CenterX=14.1421 CenterY=14.1421 CenterZ=0 NormalX=0 NormalY=0 NormalZ=1 AngleXU=0 Radius=3.2909
    g21: LineSegment StartX=-13.2904 StartY=-10.9634 StartZ=0 EndX=-16.4692 EndY=-11.8151 EndZ=0
    g22: LineSegment StartX=-16.4692 StartY=-11.8151 StartZ=0 EndX=-17.3209 EndY=-14.9939 EndZ=0
    g23: LineSegment StartX=-17.3209 StartY=-14.9939 StartZ=0 EndX=-14.9939 EndY=-17.3209 EndZ=0
    g24: LineSegment StartX=-14.9939 StartY=-17.3209 StartZ=0 EndX=-11.8151 EndY=-16.4692 EndZ=0
    g25: LineSegment StartX=-11.8151 StartY=-16.4692 StartZ=0 EndX=-10.9634 EndY=-13.2904 EndZ=0
    g26: LineSegment StartX=-10.9634 StartY=-13.2904 StartZ=0 EndX=-13.2904 EndY=-10.9634 EndZ=0
    g27: Circle [constr] CenterX=-14.1421 CenterY=-14.1421 CenterZ=0 NormalX=0 NormalY=0 NormalZ=1 AngleXU=0 Radius=3.2909
    g28: LineSegment StartX=16.4692 StartY=-11.8151 StartZ=0 EndX=13.2904 EndY=-10.9634 EndZ=0
    g29: LineSegment StartX=13.2904 StartY=-10.9634 StartZ=0 EndX=10.9634 EndY=-13.2904 EndZ=0
    g30: LineSegment StartX=10.9634 StartY=-13.2904 StartZ=0 EndX=11.8151 EndY=-16.4692 EndZ=0
    g31: LineSegment StartX=11.8151 StartY=-16.4692 StartZ=0 EndX=14.9939 EndY=-17.3209 EndZ=0
    g32: LineSegment StartX=14.9939 StartY=-17.3209 StartZ=0 EndX=17.3209 EndY=-14.9939 EndZ=0
    g33: LineSegment StartX=17.3209 StartY=-14.9939 StartZ=0 EndX=16.4692 EndY=-11.8151 EndZ=0
    g34: Circle [constr] CenterX=14.1421 CenterY=-14.1421 CenterZ=0 NormalX=0 NormalY=0 NormalZ=1 AngleXU=0 Radius=3.2909
  constraints (84):
    c: Coincident(g0,g-1)
    c: Radius(g0) = 20
    c: PointOnObject(g1,g0)
    c: PointOnObject(g1,g0)
    c: PointOnObject(g2,g0)
    c: PointOnObject(g2,g0)
    c: PointOnObject(g-1,g2)
    c: PointOnObject(g-1,g1)
    c: Perpendicular(g1,g2)
    c: Coincident(g3,g4)
    c: Coincident(g4,g5)
    c: Coincident(g5,g6)
    c: Coincident(g6,g3)
    c: Horizontal(g3)
    c: Horizontal(g5)
    c: Vertical(g4)
    c: Vertical(g6)
    c: Coincident(g3,g1)
    c: Coincident(g4,g1)
    c: Equal(g3,g4)
    c: Coincident(g7,g8)
    c: Coincident(g8,g9)
    c: Coincident(g9,g10)
    c: Coincident(g10,g11)
    c: Coincident(g11,g12)
    c: Coincident(g12,g7)
    c: Equal(g7, g8-g12) x5
    c: PointOnObject(g7,g13)
    c: PointOnObject(g8,g13)
    c: PointOnObject(g9,g13)
    c: PointOnObject(g10,g13)
    c: PointOnObject(g11,g13)
    c: PointOnObject(g12,g13)
    c: Coincident(g13,g1)
    c: Coincident(g14,g15)
    c: Coincident(g15,g16)
    c: Coincident(g16,g17)
    c: Coincident(g17,g18)
    c: Coincident(g18,g19)
    c: Coincident(g19,g14)
    c: Equal(g14, g15-g19) x5
    c: PointOnObject(g14,g20)
    c: PointOnObject(g15,g20)
    c: PointOnObject(g16,g20)
    c: PointOnObject(g17,g20)
    c: PointOnObject(g18,g20)
    c: PointOnObject(g19,g20)
    c: Coincident(g20,g2)
    c: Coincident(g21,g22)
    c: Coincident(g22,g23)
    c: Coincident(g23,g24)
    c: Coincident(g24,g25)
    c: Coincident(g25,g26)
    c: Coincident(g26,g21)
    c: Equal(g21, g22-g26) x5
    c: PointOnObject(g21,g27)
    c: PointOnObject(g22,g27)
    c: PointOnObject(g23,g27)
    c: PointOnObject(g24,g27)
    c: PointOnObject(g25,g27)
    c: PointOnObject(g26,g27)
    c: Coincident(g27,g2)
    c: Perpendicular(g1,g11)
    c: Perpendicular(g2,g16)
    c: Perpendicular(g2,g26)
    c: Coincident(g28,g29)
    c: Coincident(g29,g30)
    c: Coincident(g30,g31)
    c: Coincident(g31,g32)
    c: Coincident(g32,g33)
    c: Coincident(g33,g28)
    c: Equal(g28, g29-g33) x5
    c: PointOnObject(g28,g34)
    c: PointOnObject(g29,g34)
    c: PointOnObject(g30,g34)
    c: PointOnObject(g31,g34)
    c: PointOnObject(g32,g34)
    c: PointOnObject(g33,g34)
    c: Coincident(g34,g1)
    c: Perpendicular(g1,g29)
    c: Equal(g20,g13)
    c: Equal(g13,g27)
    c: Equal(g27,g34)
    c: Distance(g15,g14) = 5.7
FEATURE [PartDesign::Pocket] Pocket728  label="Nutholes Servohorn Cap003"
  BaseFeature = -> Pocket707
  Length = 2.5
  Length2 = 100
  Profile = -> Sketch1923
  Type = 0
FEATURE [Sketcher::SketchObject] Sketch1910
  MapMode = 5
  Placement = pos=(0,-28.25,0) rot=(1,0,0;1.5708rad)
  Support = -> [Pocket728]
  sketch-geometry (8):
    g0: LineSegment StartX=3.75 StartY=22.9 StartZ=0 EndX=6.75 EndY=22.9 EndZ=0
    g1: LineSegment StartX=6.75 StartY=22.9 StartZ=0 EndX=6.75 EndY=17.1 EndZ=0
    g2: LineSegment StartX=6.75 StartY=17.1 StartZ=0 EndX=3.75 EndY=17.1 EndZ=0
    g3: LineSegment StartX=3.75 StartY=17.1 StartZ=0 EndX=3.75 EndY=22.9 EndZ=0
    g4: LineSegment StartX=3.75 StartY=12.9 StartZ=0 EndX=6.75 EndY=12.9 EndZ=0
    g5: LineSegment StartX=6.75 StartY=12.9 StartZ=0 EndX=6.75 EndY=7.1 EndZ=0
    g6: LineSegment StartX=6.75 StartY=7.1 StartZ=0 EndX=3.75 EndY=7.1 EndZ=0
    g7: LineSegment StartX=3.75 StartY=7.1 StartZ=0 EndX=3.75 EndY=12.9 EndZ=0
  constraints (24):
    c: Coincident(g0,g1)
    c: Coincident(g1,g2)
    c: Coincident(g2,g3)
    c: Coincident(g3,g0)
    c: Horizontal(g0)
    c: Horizontal(g2)
    c: Vertical(g1)
    c: Vertical(g3)
    c: Coincident(g4,g5)
    c: Coincident(g5,g6)
    c: Coincident(g6,g7)
    c: Coincident(g7,g4)
    c: Horizontal(g4)
    c: Horizontal(g6)
    c: Vertical(g5)
    c: Vertical(g7)
    c: Equal(g0,g4)
    c: Equal(g1,g5)
    c: DistanceY(g1,g1) = 5.8
    c: DistanceY(g4,g1) = 4.2
    c: DistanceX(g-1,g5) = 6.75
    c: DistanceX(g0,g0) = 3
    c: Vertical(g4,g1)
    c: DistanceY(g-1,g5) = 7.1
FEATURE [PartDesign::Pocket] Pocket732  label="Nutholes Servo Pocket003"
  BaseFeature = -> Pocket728
  Length = 56.5
  Length2 = 100
  Profile = -> Sketch1910
  Type = 0
FEATURE [Sketcher::SketchObject] Sketch1916
  MapMode = 5
  Placement = pos=(9.75,0,0) rot=(0.57735,0.57735,0.57735;2.0944rad)
  Support = -> [Pocket732]
  sketch-geometry (4):
    g0: Circle CenterX=-24.25 CenterY=20 CenterZ=0 NormalX=0 NormalY=0 NormalZ=1 AngleXU=0 Radius=1.6
    g1: Circle CenterX=-24.25 CenterY=10 CenterZ=0 NormalX=0 NormalY=0 NormalZ=1 AngleXU=0 Radius=1.6
    g2: Circle CenterX=24.25 CenterY=20 CenterZ=0 NormalX=0 NormalY=0 NormalZ=1 AngleXU=0 Radius=1.6
    g3: Circle CenterX=24.25 CenterY=10 CenterZ=0 NormalX=0 NormalY=0 NormalZ=1 AngleXU=0 Radius=1.6
  constraints (11):
    c: Vertical(g3,g2)
    c: Vertical(g1,g0)
    c: Symmetric(g0,g2,g-2)
    c: Radius(g0) = 1.6
    c: Equal(g0,g1)
    c: Equal(g0,g2)
    c: Equal(g0,g3)
    c: DistanceY(g3,g2) = 10
    c: Horizontal(g1,g3)
    c: DistanceY(g-1,g3) = 10
    c: DistanceX(g0,g2) = 48.5
FEATURE [PartDesign::Pocket] Pocket730  label="Screwholes Servo Pocket003"
  BaseFeature = -> Pocket732
  Length = 18
  Length2 = 100
  Profile = -> Sketch1916
  Type = 0
FEATURE [Sketcher::SketchObject] Sketch1921
  MapMode = 5
  Placement = pos=(-18.75,0,0) rot=(0.57735,0.57735,0.57735;2.0944rad)
  Support = -> [Pocket730]
  sketch-geometry (1):
    g0: Circle CenterX=10 CenterY=15 CenterZ=0 NormalX=0 NormalY=0 NormalZ=1 AngleXU=0 Radius=0.95
  constraints (3):
    c: DistanceY(g-1,g0) = 15
    c: DistanceX(g-1,g0) = 10
    c: Radius(g0) = 0.95
FEATURE [PartDesign::Pocket] Pocket733  label="Screwhole Ball Bearing Pin003"
  BaseFeature = -> Pocket730
  Length = 3
  Length2 = 100
  Profile = -> Sketch1921
  Type = 0
FEATURE [Sketcher::SketchObject] Sketch1920
  MapMode = 5
  Placement = pos=(-18.75,0,0) rot=(0.57735,0.57735,0.57735;2.0944rad)
  Support = -> [Pocket733]
  sketch-geometry (7):
    g0: LineSegment StartX=12.05 StartY=13.8164 StartZ=0 EndX=12.05 EndY=16.1836 EndZ=0
    g1: LineSegment StartX=12.05 StartY=16.1836 StartZ=0 EndX=10 EndY=17.3671 EndZ=0
    g2: LineSegment StartX=10 StartY=17.3671 StartZ=0 EndX=7.95 EndY=16.1836 EndZ=0
    g3: LineSegment StartX=7.95 StartY=16.1836 StartZ=0 EndX=7.95 EndY=13.8164 EndZ=0
    g4: LineSegment StartX=7.95 StartY=13.8164 StartZ=0 EndX=10 EndY=12.6329 EndZ=0
    g5: LineSegment StartX=10 StartY=12.6329 StartZ=0 EndX=12.05 EndY=13.8164 EndZ=0
    g6: Circle [constr] CenterX=10 CenterY=15 CenterZ=0 NormalX=0 NormalY=0 NormalZ=1 AngleXU=0 Radius=2.36714
  constraints (17):
    c: Coincident(g0,g1)
    c: Coincident(g1,g2)
    c: Coincident(g2,g3)
    c: Coincident(g3,g4)
    c: Coincident(g4,g5)
    c: Coincident(g5,g0)
    c: Equal(g0, g1-g5) x5
    c: PointOnObject(g0,g6)
    c: PointOnObject(g1,g6)
    c: PointOnObject(g2,g6)
    c: PointOnObject(g3,g6)
    c: PointOnObject(g4,g6)
    c: PointOnObject(g5,g6)
    c: Vertical(g3)
    c: DistanceX(g-1,g6) = 10
    c: DistanceY(g-1,g6) = 15
    c: Distance(g0,g4) = 4.1
FEATURE [PartDesign::Pocket] Pocket726  label="Nuthole Ball Bearing Pin003"
  BaseFeature = -> Pocket733
  Length = 1.5
  Length2 = 100
  Profile = -> Sketch1920
  Type = 0
FEATURE [Sketcher::SketchObject] Sketch1911
  MapMode = 5
  Placement = pos=(0,28.25,0) rot=(0,0.707107,0.707107;3.14159rad)
  Support = -> [Pocket726]
  sketch-geometry (4):
    g0: LineSegment StartX=9.25 StartY=25 StartZ=0 EndX=14.25 EndY=25 EndZ=0
    g1: LineSegment StartX=14.25 StartY=25 StartZ=0 EndX=14.25 EndY=11.5 EndZ=0
    g2: ArcOfCircle CenterX=11.75 CenterY=11.5 CenterZ=0 NormalX=0 NormalY=0 NormalZ=1 AngleXU=0 Radius=2.5 StartAngle=3.14159 EndAngle=6.28319
    g3: LineSegment StartX=9.25 StartY=11.5 StartZ=0 EndX=9.25 EndY=25 EndZ=0
  constraints (11):
    c: Horizontal(g0)
    c: Coincident(g0,g1)
    c: Vertical(g1)
    c: Tangent(g1,g2) = 1.5708
    c: Tangent(g2,g3) = 1.5708
    c: Coincident(g3,g0)
    c: DistanceX(g0,g0) = 5
    c: Vertical(g3)
    c: DistanceX(g-1,g2) = 11.75
    c: DistanceY(g-1,g2) = 11.5
    c: DistanceY(g1,g1) = 13.5
FEATURE [PartDesign::Pocket] Pocket722  label="Servocable014"
  BaseFeature = -> Pocket726
  Length = 8
  Length2 = 100
  Profile = -> Sketch1911
  Type = 0
FEATURE [PartDesign::Fillet] Fillet241  label="Smooth Servo Pocket Edges003"
  Base = -> Pocket722 [Edge62,Edge137,Edge61,Edge146,Edge60]
  BaseFeature = -> Pocket722
  Radius = 1
FEATURE [PartDesign::Fillet] Fillet243  label="Smooth Servocable Edges008"
  Base = -> Fillet241 [Edge10,Edge165]
  BaseFeature = -> Fillet241
  Radius = 2.5
FEATURE [PartDesign::Body] Body542  label="Shoulder_Joint_Servomount003"
  Group = -> [Sketch1922,Pad866,Pad861,Sketch1918,Pocket723,Sketch1919,Pocket719,Sketch1917,Pocket707,Sketch1923,Pocket728,Sketch1910,Pocket732,Sketch1916,Pocket730,Sketch1921,Pocket733,Sketch1920,Pocket726,Sketch1911,Pocket722,Fillet241,Fillet243]
  Origin = -> Origin763
  Tip = -> Fillet243
FEATURE [Sketcher::SketchObject] Sketch1925
  MapMode = 5
  Placement = pos=(0,0,12) rot=(0,0,1;0rad)
  Support = -> [Pad867]
  sketch-geometry (9):
    g0: Circle [constr] CenterX=0 CenterY=0 CenterZ=0 NormalX=0 NormalY=0 NormalZ=1 AngleXU=0 Radius=20
    g1: LineSegment [constr] StartX=-14.1421 StartY=14.1421 StartZ=0 EndX=14.1421 EndY=14.1421 EndZ=0
    g2: LineSegment [constr] StartX=14.1421 StartY=14.1421 StartZ=0 EndX=14.1421 EndY=-14.1421 EndZ=0
    g3: LineSegment [constr] StartX=14.1421 StartY=-14.1421 StartZ=0 EndX=-14.1421 EndY=-14.1421 EndZ=0
    g4: LineSegment [constr] StartX=-14.1421 StartY=-14.1421 StartZ=0 EndX=-14.1421 EndY=14.1421 EndZ=0
    g5: Circle CenterX=-14.1421 CenterY=14.1421 CenterZ=0 NormalX=0 NormalY=0 NormalZ=1 AngleXU=0 Radius=1.6
    g6: Circle CenterX=14.1421 CenterY=14.1421 CenterZ=0 NormalX=0 NormalY=0 NormalZ=1 AngleXU=0 Radius=1.6
    g7: Circle CenterX=14.1421 CenterY=-14.1421 CenterZ=0 NormalX=0 NormalY=0 NormalZ=1 AngleXU=0 Radius=1.6
    g8: Circle CenterX=-14.1421 CenterY=-14.1421 CenterZ=0 NormalX=0 NormalY=0 NormalZ=1 AngleXU=0 Radius=1.6
  constraints (22):
    c: Coincident(g0,g-1)
    c: Radius(g0) = 20
    c: Coincident(g1,g2)
    c: Coincident(g2,g3)
    c: Coincident(g3,g4)
    c: Coincident(g4,g1)
    c: Horizontal(g1)
    c: Horizontal(g3)
    c: Vertical(g2)
    c: Vertical(g4)
    c: PointOnObject(g1,g0)
    c: PointOnObject(g2,g0)
    c: PointOnObject(g1,g0)
    c: Equal(g1,g2)
    c: Coincident(g5,g1)
    c: Coincident(g6,g1)
    c: Coincident(g7,g2)
    c: Coincident(g8,g3)
    c: Equal(g8,g5)
    c: Equal(g5,g6)
    c: Equal(g6,g7)
    c: Radius(g6) = 1.6
FEATURE [PartDesign::Pocket] Pocket724  label="Screwholes Mounting003"
  BaseFeature = -> Pad867
  Length = 12
  Length2 = 100
  Profile = -> Sketch1925
  Type = 0
FEATURE [Sketcher::SketchObject] Sketch1927
  MapMode = 5
  Support = -> [XY_Plane739]
FEATURE [Sketcher::SketchObject] Sketch1929
  MapMode = 5
  Support = -> [XY_Plane745]
FEATURE [Sketcher::SketchObject] Sketch1930
  MapMode = 5
  Support = -> [XY_Plane771]
  sketch-geometry (1):
    g0: Circle CenterX=0 CenterY=0 CenterZ=0 NormalX=0 NormalY=0 NormalZ=1 AngleXU=0 Radius=1.9
  constraints (2):
    c: Coincident(g0,g-1)
    c: Radius(g0) = 1.9
FEATURE [PartDesign::Pad] Pad835  label="M3x8 Head102"
  Length = 2
  Length2 = 100
  Profile = -> Sketch1930
  Type = 0
FEATURE [Sketcher::SketchObject] Sketch1931
  MapMode = 5
  Support = -> [XY_Plane737]
  sketch-geometry (64):
    g0: LineSegment [constr] StartX=-3.75 StartY=6.49519 StartZ=0 EndX=-7.5 EndY=0 EndZ=0
    g1: LineSegment [constr] StartX=-7.5 StartY=0 StartZ=0 EndX=-3.75 EndY=-6.49519 EndZ=0
    g2: LineSegment [constr] StartX=-3.75 StartY=-6.49519 StartZ=0 EndX=3.75 EndY=-6.49519 EndZ=0
    g3: LineSegment [constr] StartX=3.75 StartY=-6.49519 StartZ=0 EndX=7.5 EndY=0 EndZ=0
    g4: LineSegment [constr] StartX=7.5 StartY=0 StartZ=0 EndX=3.75 EndY=6.49519 EndZ=0
    g5: LineSegment [constr] StartX=3.75 StartY=6.49519 StartZ=0 EndX=-3.75 EndY=6.49519 EndZ=0
    g6: Circle [constr] CenterX=0 CenterY=0 CenterZ=0 NormalX=0 NormalY=0 NormalZ=1 AngleXU=0 Radius=7.5
    g7: LineSegment [constr] StartX=0 StartY=7.5 StartZ=0 EndX=-6.49519 EndY=3.75 EndZ=0
    g8: LineSegment [constr] StartX=-6.49519 StartY=3.75 StartZ=0 EndX=-6.49519 EndY=-3.75 EndZ=0
    g9: LineSegment [constr] StartX=-6.49519 StartY=-3.75 StartZ=0 EndX=9.8e-15 EndY=-7.5 EndZ=0
    g10: LineSegment [constr] StartX=9.8e-15 StartY=-7.5 StartZ=0 EndX=6.49519 EndY=-3.75 EndZ=0
    g11: LineSegment [constr] StartX=6.49519 StartY=-3.75 StartZ=0 EndX=6.49519 EndY=3.75 EndZ=0
    g12: LineSegment [constr] StartX=6.49519 StartY=3.75 StartZ=0 EndX=0 EndY=7.5 EndZ=0
    g13: Circle [constr] CenterX=0 CenterY=0 CenterZ=0 NormalX=0 NormalY=0 NormalZ=1 AngleXU=0 Radius=7.5
    g14: LineSegment [constr] StartX=0 StartY=10.5 StartZ=0 EndX=-9.09327 EndY=5.25 EndZ=0
    g15: LineSegment [constr] StartX=-9.09327 StartY=5.25 StartZ=0 EndX=-9.09327 EndY=-5.25 EndZ=0
    g16: LineSegment [constr] StartX=-9.09327 StartY=-5.25 StartZ=0 EndX=-1.42e-14 EndY=-10.5 EndZ=0
    g17: LineSegment [constr] StartX=-1.42e-14 StartY=-10.5 StartZ=0 EndX=9.09327 EndY=-5.25 EndZ=0
    g18: LineSegment [constr] StartX=9.09327 StartY=-5.25 StartZ=0 EndX=9.09327 EndY=5.25 EndZ=0
    g19: LineSegment [constr] StartX=9.09327 StartY=5.25 StartZ=0 EndX=0 EndY=10.5 EndZ=0
    g20: Circle [constr] CenterX=0 CenterY=0 CenterZ=0 NormalX=0 NormalY=0 NormalZ=1 AngleXU=0 Radius=10.5
    g21: LineSegment [constr] StartX=0 StartY=13.5 StartZ=0 EndX=-11.6913 EndY=6.75 EndZ=0
    g22: LineSegment [constr] StartX=-11.6913 StartY=6.75 StartZ=0 EndX=-11.6913 EndY=-6.75 EndZ=0
    g23: LineSegment [constr] StartX=-11.6913 StartY=-6.75 StartZ=0 EndX=0 EndY=-13.5 EndZ=0
    g24: LineSegment [constr] StartX=0 StartY=-13.5 StartZ=0 EndX=11.6913 EndY=-6.75 EndZ=0
    g25: LineSegment [constr] StartX=11.6913 StartY=-6.75 StartZ=0 EndX=11.6913 EndY=6.75 EndZ=0
    g26: LineSegment [constr] StartX=11.6913 StartY=6.75 StartZ=0 EndX=0 EndY=13.5 EndZ=0
    g27: Circle [constr] CenterX=0 CenterY=0 CenterZ=0 NormalX=0 NormalY=0 NormalZ=1 AngleXU=0 Radius=13.5
    g28: ArcOfCircle CenterX=0 CenterY=13.5 CenterZ=0 NormalX=0 NormalY=0 NormalZ=1 AngleXU=0 Radius=2.5 StartAngle=0.171439 EndAngle=2.97015
    g29: ArcOfCircle CenterX=11.6913 CenterY=6.75 CenterZ=0 NormalX=0 NormalY=0 NormalZ=1 AngleXU=0 Radius=2.5 StartAngle=5.40743 EndAngle=8.20614
    g30: ArcOfCircle CenterX=11.6913 CenterY=-6.75 CenterZ=0 NormalX=0 NormalY=0 NormalZ=1 AngleXU=0 Radius=2.5 StartAngle=4.36023 EndAngle=7.15894
    g31: ArcOfCircle CenterX=0 CenterY=-13.5 CenterZ=0 NormalX=0 NormalY=0 NormalZ=1 AngleXU=0 Radius=2.5 StartAngle=3.31303 EndAngle=6.11175
    g32: ArcOfCircle CenterX=-11.6913 CenterY=-6.75 CenterZ=0 NormalX=0 NormalY=0 NormalZ=1 AngleXU=0 Radius=2.5 StartAngle=2.26583 EndAngle=5.06455
    g33: ArcOfCircle CenterX=-11.6913 CenterY=6.75 CenterZ=0 NormalX=0 NormalY=0 NormalZ=1 AngleXU=0 Radius=2.5 StartAngle=1.21864 EndAngle=4.01735
    g34: LineSegment StartX=-10.829 StartY=9.09658 StartZ=0 EndX=-3.75 EndY=6.49519 EndZ=0
    g35: LineSegment StartX=-3.75 StartY=6.49519 StartZ=0 EndX=-2.46335 EndY=13.9265 EndZ=0
    g36: LineSegment StartX=2.46335 StartY=13.9265 StartZ=0 EndX=3.75 EndY=6.49519 EndZ=0
    g37: LineSegment StartX=3.75 StartY=6.49519 StartZ=0 EndX=10.829 EndY=9.09658 EndZ=0
    g38: LineSegment StartX=13.2924 StartY=4.82993 StartZ=0 EndX=7.5 EndY=0 EndZ=0
    g39: LineSegment StartX=7.5 StartY=0 StartZ=0 EndX=13.2924 EndY=-4.82993 EndZ=0
    g40: LineSegment StartX=10.829 StartY=-9.09658 StartZ=0 EndX=3.75 EndY=-6.49519 EndZ=0
    g41: LineSegment StartX=3.75 StartY=-6.49519 StartZ=0 EndX=2.46335 EndY=-13.9265 EndZ=0
    g42: LineSegment StartX=-2.46335 StartY=-13.9265 StartZ=0 EndX=-3.75 EndY=-6.49519 EndZ=0
    g43: LineSegment StartX=-3.75 StartY=-6.49519 StartZ=0 EndX=-10.829 EndY=-9.09658 EndZ=0
    g44: LineSegment StartX=-13.2924 StartY=-4.82993 StartZ=0 EndX=-7.5 EndY=0 EndZ=0
    g45: LineSegment StartX=-7.5 StartY=0 StartZ=0 EndX=-13.2924 EndY=4.82993 EndZ=0
    g46: Circle CenterX=-11.6913 CenterY=6.75 CenterZ=0 NormalX=0 NormalY=0 NormalZ=1 AngleXU=0 Radius=0.75
    g47: Circle CenterX=-9.09327 CenterY=5.25 CenterZ=0 NormalX=0 NormalY=0 NormalZ=1 AngleXU=0 Radius=0.75
    g48: Circle CenterX=-6.49519 CenterY=3.75 CenterZ=0 NormalX=0 NormalY=0 NormalZ=1 AngleXU=0 Radius=0.75
    g49: Circle CenterX=0 CenterY=13.5 CenterZ=0 NormalX=0 NormalY=0 NormalZ=1 AngleXU=0 Radius=0.75
    g50: Circle CenterX=0 CenterY=10.5 CenterZ=0 NormalX=0 NormalY=0 NormalZ=1 AngleXU=0 Radius=0.75
    g51: Circle CenterX=0 CenterY=7.5 CenterZ=0 NormalX=0 NormalY=0 NormalZ=1 AngleXU=0 Radius=0.75
    g52: Circle CenterX=11.6913 CenterY=6.75 CenterZ=0 NormalX=0 NormalY=0 NormalZ=1 AngleXU=0 Radius=0.75
    g53: Circle CenterX=9.09327 CenterY=5.25 CenterZ=0 NormalX=0 NormalY=0 NormalZ=1 AngleXU=0 Radius=0.75
    g54: Circle CenterX=6.49519 CenterY=3.75 CenterZ=0 NormalX=0 NormalY=0 NormalZ=1 AngleXU=0 Radius=0.75
    g55: Circle CenterX=11.6913 CenterY=-6.75 CenterZ=0 NormalX=0 NormalY=0 NormalZ=1 AngleXU=0 Radius=0.75
    g56: Circle CenterX=9.09327 CenterY=-5.25 CenterZ=0 NormalX=0 NormalY=0 NormalZ=1 AngleXU=0 Radius=0.75
    g57: Circle CenterX=6.49519 CenterY=-3.75 CenterZ=0 NormalX=0 NormalY=0 NormalZ=1 AngleXU=0 Radius=0.75
    g58: Circle CenterX=9.8e-15 CenterY=-7.5 CenterZ=0 NormalX=0 NormalY=0 NormalZ=1 AngleXU=0 Radius=0.75
    g59: Circle CenterX=-1.42e-14 CenterY=-10.5 CenterZ=0 NormalX=0 NormalY=0 NormalZ=1 AngleXU=0 Radius=0.75
    g60: Circle CenterX=0 CenterY=-13.5 CenterZ=0 NormalX=0 NormalY=0 NormalZ=1 AngleXU=0 Radius=0.75
    g61: Circle CenterX=-11.6913 CenterY=-6.75 CenterZ=0 NormalX=0 NormalY=0 NormalZ=1 AngleXU=0 Radius=0.75
    g62: Circle CenterX=-9.09327 CenterY=-5.25 CenterZ=0 NormalX=0 NormalY=0 NormalZ=1 AngleXU=0 Radius=0.75
    g63: Circle CenterX=-6.49519 CenterY=-3.75 CenterZ=0 NormalX=0 NormalY=0 NormalZ=1 AngleXU=0 Radius=0.75
  constraints (136):
    c: Coincident(g0,g1)
    c: Coincident(g1,g2)
    c: Coincident(g2,g3)
    c: Coincident(g3,g4)
    c: Coincident(g4,g5)
    c: Coincident(g5,g0)
    c: Equal(g0, g1-g5) x5
    c: PointOnObject(g0,g6)
    c: PointOnObject(g1,g6)
    c: PointOnObject(g2,g6)
    c: PointOnObject(g3,g6)
    c: PointOnObject(g4,g6)
    c: PointOnObject(g5,g6)
    c: Coincident(g6,g-1)
    c: Coincident(g7,g8)
    c: Coincident(g8,g9)
    c: Coincident(g9,g10)
    c: Coincident(g10,g11)
    c: Coincident(g11,g12)
    c: Coincident(g12,g7)
    c: Equal(g7, g8-g12) x5
    c: PointOnObject(g7,g13)
    c: PointOnObject(g8,g13)
    c: PointOnObject(g9,g13)
    c: PointOnObject(g10,g13)
    c: PointOnObject(g11,g13)
    c: PointOnObject(g12,g13)
    c: Coincident(g13,g-1)
    c: PointOnObject(g12,g6)
    c: PointOnObject(g7,g-2)
    c: Horizontal(g5)
    c: Radius(g6) = 7.5
    c: Coincident(g14,g15)
    c: Coincident(g15,g16)
    c: Coincident(g16,g17)
    c: Coincident(g17,g18)
    c: Coincident(g18,g19)
    c: Coincident(g19,g14)
    c: Equal(g14, g15-g19) x5
    c: PointOnObject(g14,g20)
    c: PointOnObject(g15,g20)
    c: PointOnObject(g16,g20)
    c: PointOnObject(g17,g20)
    c: PointOnObject(g18,g20)
    c: PointOnObject(g19,g20)
    c: Coincident(g20,g-1)
    c: PointOnObject(g19,g-2)
    c: Radius(g20) = 10.5
    c: Coincident(g21,g22)
    c: Coincident(g22,g23)
    c: Coincident(g23,g24)
    c: Coincident(g24,g25)
    c: Coincident(g25,g26)
    c: Coincident(g26,g21)
    c: Equal(g21, g22-g26) x5
    c: PointOnObject(g21,g27)
    c: PointOnObject(g22,g27)
    c: PointOnObject(g23,g27)
    c: PointOnObject(g24,g27)
    c: PointOnObject(g25,g27)
    c: PointOnObject(g26,g27)
    c: Coincident(g27,g-1)
    c: PointOnObject(g26,g-2)
    c: Radius(g27) = 13.5
    c: Coincident(g28,g21)
    c: Coincident(g29,g25)
    c: Coincident(g30,g24)
    c: Coincident(g31,g23)
    c: Coincident(g32,g22)
    c: Coincident(g33,g21)
    c: Coincident(g34,g0)
    c: Coincident(g35,g34)
    c: Coincident(g36,g4)
    c: Coincident(g37,g36)
    c: Coincident(g38,g3)
    c: Coincident(g39,g38)
    c: Coincident(g40,g2)
    c: Coincident(g41,g40)
    c: Coincident(g42,g1)
    c: Coincident(g43,g42)
    c: Coincident(g44,g0)
    c: Coincident(g45,g44)
    c: Tangent(g35,g28) = 1.5708
    c: Tangent(g36,g28) = 1.5708
    c: Tangent(g37,g29) = 1.5708
    c: Tangent(g38,g29) = 1.5708
    c: Tangent(g39,g30) = 1.5708
    c: Tangent(g40,g30) = 1.5708
    c: Tangent(g41,g31) = 1.5708
    c: Tangent(g42,g31) = 1.5708
    c: Tangent(g43,g32) = 1.5708
    c: Tangent(g44,g32) = 1.5708
    c: Tangent(g45,g33) = 1.5708
    c: Tangent(g34,g33) = 1.5708
    c: Radius(g29) = 2.5
    c: Equal(g29,g28)
    c: Equal(g28,g33)
    c: Equal(g33,g32)
    c: Equal(g32,g31)
    c: Equal(g31,g30)
    c: Coincident(g46,g33)
    c: Coincident(g47,g14)
    c: Coincident(g48,g7)
    c: Coincident(g49,g28)
    c: Coincident(g50,g14)
    c: Coincident(g51,g7)
    c: Coincident(g52,g29)
    c: Coincident(g53,g18)
    c: Coincident(g54,g11)
    c: Coincident(g55,g30)
    c: Coincident(g56,g17)
    c: Coincident(g57,g10)
    c: Coincident(g58,g9)
    c: Coincident(g59,g16)
    c: Coincident(g60,g31)
    c: Coincident(g61,g32)
    c: Coincident(g62,g15)
    c: Coincident(g63,g8)
    c: Equal(g61,g62)
    c: Equal(g62,g63)
    c: Equal(g63,g58)
    c: Equal(g58,g59)
    c: Equal(g59,g60)
    c: Equal(g60,g55)
    c: Equal(g55,g56)
    c: Equal(g56,g57)
    c: Equal(g57,g54)
    c: Equal(g54,g53)
    c: Equal(g53,g52)
    c: Equal(g52,g51)
    c: Equal(g51,g50)
    c: Equal(g50,g49)
    c: Equal(g49,g46)
    c: Equal(g46,g47)
    c: Equal(g47,g48)
    c: Radius(g55) = 0.75
FEATURE [PartDesign::Pad] Pad844
  Length = 2
  Length2 = 100
  Profile = -> Sketch1931
  Type = 0
FEATURE [Sketcher::SketchObject] Sketch1913
  MapMode = 5
  Placement = pos=(0,0,2) rot=(0,0,1;0rad)
  Support = -> [Pad844]
  sketch-geometry (2):
    g0: Circle CenterX=0 CenterY=0 CenterZ=0 NormalX=0 NormalY=0 NormalZ=1 AngleXU=0 Radius=5
    g1: Circle CenterX=0 CenterY=0 CenterZ=0 NormalX=0 NormalY=0 NormalZ=1 AngleXU=0 Radius=3.5
  constraints (4):
    c: Coincident(g0,g-1)
    c: Coincident(g1,g0)
    c: Radius(g1) = 3.5
    c: Radius(g0) = 5
FEATURE [PartDesign::Pocket] Pocket711
  BaseFeature = -> Pad844
  Length = 1
  Length2 = 100
  Profile = -> Sketch1913
  Type = 0
FEATURE [Sketcher::SketchObject] Sketch1924
  MapMode = 5
  Placement = pos=(0,0,2) rot=(0,0,1;0rad)
  Support = -> [Pocket711]
  sketch-geometry (1):
    g0: Circle CenterX=0 CenterY=0 CenterZ=0 NormalX=0 NormalY=0 NormalZ=1 AngleXU=0 Radius=3
  constraints (2):
    c: Coincident(g0,g-1)
    c: Radius(g0) = 3
FEATURE [PartDesign::Pocket] Pocket708
  BaseFeature = -> Pocket711
  Length = 1
  Length2 = 100
  Profile = -> Sketch1924
  Type = 0
FEATURE [Sketcher::SketchObject] Sketch1912
  MapMode = 5
  Placement = pos=(0,0,1) rot=(0,0,1;0rad)
  Support = -> [Pocket708]
  sketch-geometry (1):
    g0: Circle CenterX=0 CenterY=0 CenterZ=0 NormalX=0 NormalY=0 NormalZ=1 AngleXU=0 Radius=1.5
  constraints (2):
    c: Coincident(g0,g-1)
    c: Radius(g0) = 1.5
FEATURE [PartDesign::Pocket] Pocket706
  BaseFeature = -> Pocket708
  Length = 5
  Length2 = 100
  Profile = -> Sketch1912
  Type = 0
FEATURE [Sketcher::SketchObject] Sketch1933
  MapMode = 5
  Support = -> [XY_Plane739]
FEATURE [Sketcher::SketchObject] Sketch1934
  MapMode = 5
  Support = -> [XY_Plane767]
  sketch-geometry (8):
    g0: LineSegment StartX=0 StartY=2.3094 StartZ=0 EndX=-2 EndY=1.1547 EndZ=0
    g1: LineSegment StartX=-2 StartY=1.1547 StartZ=0 EndX=-2 EndY=-1.1547 EndZ=0
    g2: LineSegment StartX=-2 StartY=-1.1547 StartZ=0 EndX=-2e-16 EndY=-2.3094 EndZ=0
    g3: LineSegment StartX=-2e-16 StartY=-2.3094 StartZ=0 EndX=2 EndY=-1.1547 EndZ=0
    g4: LineSegment StartX=2 StartY=-1.1547 StartZ=0 EndX=2 EndY=1.1547 EndZ=0
    g5: LineSegment StartX=2 StartY=1.1547 StartZ=0 EndX=0 EndY=2.3094 EndZ=0
    g6: Circle [constr] CenterX=0 CenterY=0 CenterZ=0 NormalX=0 NormalY=0 NormalZ=1 AngleXU=0 Radius=2.3094
    g7: Circle CenterX=0 CenterY=0 CenterZ=0 NormalX=0 NormalY=0 NormalZ=1 AngleXU=0 Radius=1
  constraints (18):
    c: Coincident(g0,g1)
    c: Coincident(g1,g2)
    c: Coincident(g2,g3)
    c: Coincident(g3,g4)
    c: Coincident(g4,g5)
    c: Coincident(g5,g0)
    c: Equal(g0, g1-g5) x5
    c: PointOnObject(g0,g6)
    c: PointOnObject(g1,g6)
    c: PointOnObject(g2,g6)
    c: PointOnObject(g3,g6)
    c: PointOnObject(g4,g6)
    c: PointOnObject(g5,g6)
    c: Coincident(g6,g-1)
    c: PointOnObject(g5,g-2)
    c: DistanceX(g0,g4) = 4
    c: Coincident(g7,g-1)
    c: Radius(g7) = 1
FEATURE [PartDesign::Pad] Pad845  label="M3 Nut Primitive165"
  Length = 0.6
  Length2 = 0.6
  Profile = -> Sketch1934
  Type = 4
FEATURE [Sketcher::SketchObject] Sketch1935
  MapMode = 5
  Support = -> [XY_Plane761]
  sketch-geometry (1):
    g0: Circle CenterX=0 CenterY=0 CenterZ=0 NormalX=0 NormalY=0 NormalZ=1 AngleXU=0 Radius=1.9
  constraints (2):
    c: Coincident(g0,g-1)
    c: Radius(g0) = 1.9
FEATURE [PartDesign::Pad] Pad840  label="M3x8 Head105"
  Length = 2
  Length2 = 100
  Profile = -> Sketch1935
  Type = 0
FEATURE [Sketcher::SketchObject] Sketch1936
  MapMode = 5
  Placement = pos=(0,0,12) rot=(0,0,1;0rad)
  Support = -> [Pocket724]
  sketch-geometry (1):
    g0: Circle CenterX=0 CenterY=0 CenterZ=0 NormalX=0 NormalY=0 NormalZ=1 AngleXU=0 Radius=16.5
  constraints (2):
    c: Coincident(g0,g-1)
    c: Radius(g0) = 16.5
FEATURE [PartDesign::Pocket] Pocket734  label="Accesshole003"
  BaseFeature = -> Pocket724
  Length = 7
  Length2 = 100
  Profile = -> Sketch1936
  Type = 0
FEATURE [Sketcher::SketchObject] Sketch1914
  MapMode = 5
  Placement = pos=(0,0,5) rot=(0,0,1;0rad)
  Support = -> [Pocket734]
  sketch-geometry (1):
    g0: Circle CenterX=0 CenterY=0 CenterZ=0 NormalX=0 NormalY=0 NormalZ=1 AngleXU=0 Radius=6.15
  constraints (2):
    c: Coincident(g0,g-1)
    c: Radius(g0) = 6.15
FEATURE [PartDesign::Pocket] Pocket729  label="Servohole003"
  BaseFeature = -> Pocket734
  Length = 5
  Length2 = 100
  Profile = -> Sketch1914
  Type = 0
FEATURE [Sketcher::SketchObject] Sketch1932
  MapMode = 5
  Placement = pos=(0,0,5) rot=(0,0,1;0rad)
  Support = -> [Pocket729]
  sketch-geometry (32):
    g0: LineSegment [constr] StartX=3.75 StartY=6.49519 StartZ=0 EndX=-3.75 EndY=6.49519 EndZ=0
    g1: LineSegment [constr] StartX=-3.75 StartY=6.49519 StartZ=0 EndX=-7.5 EndY=9e-16 EndZ=0
    g2: LineSegment [constr] StartX=-7.5 StartY=9e-16 StartZ=0 EndX=-3.75 EndY=-6.49519 EndZ=0
    g3: LineSegment [constr] StartX=-3.75 StartY=-6.49519 StartZ=0 EndX=3.75 EndY=-6.49519 EndZ=0
    g4: LineSegment [constr] StartX=3.75 StartY=-6.49519 StartZ=0 EndX=7.5 EndY=0 EndZ=0
    g5: LineSegment [constr] StartX=7.5 StartY=0 StartZ=0 EndX=3.75 EndY=6.49519 EndZ=0
    g6: Circle [constr] CenterX=0 CenterY=0 CenterZ=0 NormalX=0 NormalY=0 NormalZ=1 AngleXU=0 Radius=7.5
    g7: LineSegment [constr] StartX=0 StartY=13.5 StartZ=0 EndX=-11.6913 EndY=6.75 EndZ=0
    g8: LineSegment [constr] StartX=-11.6913 StartY=6.75 StartZ=0 EndX=-11.6913 EndY=-6.75 EndZ=0
    g9: LineSegment [constr] StartX=-11.6913 StartY=-6.75 StartZ=0 EndX=0 EndY=-13.5 EndZ=0
    g10: LineSegment [constr] StartX=-5e-16 StartY=-13.5 StartZ=0 EndX=11.6913 EndY=-6.75 EndZ=0
    g11: LineSegment [constr] StartX=11.6913 StartY=-6.75 StartZ=0 EndX=11.6913 EndY=6.75 EndZ=0
    g12: LineSegment [constr] StartX=11.6913 StartY=6.75 StartZ=0 EndX=0 EndY=13.5 EndZ=0
    g13: Circle [constr] CenterX=0 CenterY=0 CenterZ=0 NormalX=0 NormalY=0 NormalZ=1 AngleXU=0 Radius=13.5
    g14: ArcOfCircle CenterX=0 CenterY=13.5 CenterZ=0 NormalX=0 NormalY=0 NormalZ=1 AngleXU=0 Radius=2.6 StartAngle=0.15815 EndAngle=2.98344
    g15: ArcOfCircle CenterX=11.6913 CenterY=6.75 CenterZ=0 NormalX=0 NormalY=0 NormalZ=1 AngleXU=0 Radius=2.6 StartAngle=5.39414 EndAngle=8.21943
    g16: ArcOfCircle CenterX=11.6913 CenterY=-6.75 CenterZ=0 NormalX=0 NormalY=0 NormalZ=1 AngleXU=0 Radius=2.6 StartAngle=4.34694 EndAngle=7.17223
    g17: ArcOfCircle CenterX=-5e-16 CenterY=-13.5 CenterZ=0 NormalX=0 NormalY=0 NormalZ=1 AngleXU=0 Radius=2.6 StartAngle=3.29974 EndAngle=6.12503
    g18: ArcOfCircle CenterX=-11.6913 CenterY=-6.75 CenterZ=0 NormalX=0 NormalY=0 NormalZ=1 AngleXU=0 Radius=2.6 StartAngle=2.25255 EndAngle=5.07784
    g19: ArcOfCircle CenterX=-11.6913 CenterY=6.75 CenterZ=0 NormalX=0 NormalY=0 NormalZ=1 AngleXU=0 Radius=2.6 StartAngle=1.20535 EndAngle=4.03064
    g20: LineSegment StartX=-2.56755 StartY=13.9095 StartZ=0 EndX=-3.75 EndY=6.49519 EndZ=0
    g21: LineSegment StartX=-3.75 StartY=6.49519 StartZ=0 EndX=-10.7622 EndY=9.17831 EndZ=0
    g22: LineSegment StartX=2.56755 StartY=13.9095 StartZ=0 EndX=3.75 EndY=6.49519 EndZ=0
    g23: LineSegment StartX=3.75 StartY=6.49519 StartZ=0 EndX=10.7622 EndY=9.17831 EndZ=0
    g24: LineSegment StartX=13.3297 StartY=4.73117 StartZ=0 EndX=7.5 EndY=0 EndZ=0
    g25: LineSegment StartX=7.5 StartY=0 StartZ=0 EndX=13.3297 EndY=-4.73117 EndZ=0
    g26: LineSegment StartX=10.7622 StartY=-9.17831 StartZ=0 EndX=3.75 EndY=-6.49519 EndZ=0
    g27: LineSegment StartX=3.75 StartY=-6.49519 StartZ=0 EndX=2.56755 EndY=-13.9095 EndZ=0
    g28: LineSegment StartX=-2.56755 StartY=-13.9095 StartZ=0 EndX=-3.75 EndY=-6.49519 EndZ=0
    g29: LineSegment StartX=-3.75 StartY=-6.49519 StartZ=0 EndX=-10.7622 EndY=-9.17831 EndZ=0
    g30: LineSegment StartX=-13.3297 StartY=-4.73117 StartZ=0 EndX=-7.5 EndY=9e-16 EndZ=0
    g31: LineSegment StartX=-7.5 StartY=9e-16 StartZ=0 EndX=-13.3297 EndY=4.73117 EndZ=0
  constraints (68):
    c: Coincident(g0,g1)
    c: Coincident(g1,g2)
    c: Coincident(g2,g3)
    c: Coincident(g3,g4)
    c: Coincident(g4,g5)
    c: Coincident(g5,g0)
    c: Equal(g0, g1-g5) x5
    c: PointOnObject(g0,g6)
    c: PointOnObject(g1,g6)
    c: PointOnObject(g2,g6)
    c: PointOnObject(g3,g6)
    c: PointOnObject(g4,g6)
    c: PointOnObject(g5,g6)
    c: Coincident(g6,g-1)
    c: Coincident(g7,g8)
    c: Coincident(g8,g9)
    c: Coincident(g9,g10)
    c: Coincident(g10,g11)
    c: Coincident(g11,g12)
    c: Coincident(g12,g7)
    c: Equal(g7, g8-g12) x5
    c: PointOnObject(g7,g13)
    c: PointOnObject(g8,g13)
    c: PointOnObject(g9,g13)
    c: PointOnObject(g10,g13)
    c: PointOnObject(g11,g13)
    c: PointOnObject(g12,g13)
    c: Coincident(g13,g-1)
    c: Horizontal(g0)
    c: Vertical(g8)
    c: Radius(g6) = 7.5
    c: Radius(g13) = 13.5
    c: Coincident(g14,g7)
    c: Coincident(g15,g11)
    c: Coincident(g16,g10)
    c: Coincident(g17,g9)
    c: Coincident(g18,g8)
    c: Coincident(g19,g7)
    c: Coincident(g20,g0)
    c: Coincident(g21,g20)
    c: Coincident(g22,g0)
    c: Coincident(g23,g22)
    c: Coincident(g24,g4)
    c: Coincident(g25,g24)
    c: Coincident(g26,g3)
    c: Coincident(g27,g26)
    c: Coincident(g28,g2)
    c: Coincident(g29,g28)
    c: Coincident(g31,g30)
    c: Tangent(g21,g19) = -1.5708
    c: Tangent(g20,g14) = -1.5708
    c: Tangent(g22,g14) = 1.5708
    c: Tangent(g23,g15) = 1.5708
    c: Tangent(g24,g15) = 1.5708
    c: Tangent(g25,g16) = 1.5708
    c: Tangent(g26,g16) = 1.5708
    c: Tangent(g27,g17) = 1.5708
    c: Tangent(g28,g17) = 1.5708
    c: Tangent(g29,g18) = 1.5708
    c: Tangent(g30,g18) = 1.5708
    c: Tangent(g31,g19) = 1.5708
    c: Radius(g14) = 2.6
    c: Equal(g14,g15)
    c: Equal(g15,g16)
    c: Equal(g16,g17)
    c: Equal(g17,g18)
    c: Equal(g18,g19)
    c: Coincident(g30,g1)
FEATURE [PartDesign::Pocket] Pocket725  label="Servohorn016"
  BaseFeature = -> Pocket729
  Length = 2
  Length2 = 100
  Profile = -> Sketch1932
  Type = 0
FEATURE [PartDesign::Fillet] Fillet240  label="Smooth Servohorn Corners003"
  Base = -> Pocket725 [Edge81,Edge87,Edge82,Edge88,Edge93,Edge94]
  BaseFeature = -> Pocket725
  Radius = 1
FEATURE [Sketcher::SketchObject] Sketch1937
  MapMode = 5
  Placement = pos=(0,0,3) rot=(0,0,1;0rad)
  Support = -> [Fillet240]
  sketch-geometry (13):
    g0: LineSegment [constr] StartX=0 StartY=10.5 StartZ=0 EndX=-9.09327 EndY=5.25 EndZ=0
    g1: LineSegment [constr] StartX=-9.09327 StartY=5.25 StartZ=0 EndX=-9.09327 EndY=-5.25 EndZ=0
    g2: LineSegment [constr] StartX=-9.09327 StartY=-5.25 StartZ=0 EndX=0 EndY=-10.5 EndZ=0
    g3: LineSegment [constr] StartX=0 StartY=-10.5 StartZ=0 EndX=9.09327 EndY=-5.25 EndZ=0
    g4: LineSegment [constr] StartX=9.09327 StartY=-5.25 StartZ=0 EndX=9.09327 EndY=5.25 EndZ=0
    g5: LineSegment [constr] StartX=9.09327 StartY=5.25 StartZ=0 EndX=0 EndY=10.5 EndZ=0
    g6: Circle [constr] CenterX=0 CenterY=0 CenterZ=0 NormalX=0 NormalY=0 NormalZ=1 AngleXU=0 Radius=10.5
    g7: Circle CenterX=0 CenterY=10.5 CenterZ=0 NormalX=0 NormalY=0 NormalZ=1 AngleXU=0 Radius=0.95
    g8: Circle CenterX=9.09327 CenterY=5.25 CenterZ=0 NormalX=0 NormalY=0 NormalZ=1 AngleXU=0 Radius=0.95
    g9: Circle CenterX=9.09327 CenterY=-5.25 CenterZ=0 NormalX=0 NormalY=0 NormalZ=1 AngleXU=0 Radius=0.95
    g10: Circle CenterX=0 CenterY=-10.5 CenterZ=0 NormalX=0 NormalY=0 NormalZ=1 AngleXU=0 Radius=0.95
    g11: Circle CenterX=-9.09327 CenterY=-5.25 CenterZ=0 NormalX=0 NormalY=0 NormalZ=1 AngleXU=0 Radius=0.95
    g12: Circle CenterX=-9.09327 CenterY=5.25 CenterZ=0 NormalX=0 NormalY=0 NormalZ=1 AngleXU=0 Radius=0.95
  constraints (24):
    c: Coincident(g0,g1)
    c: Coincident(g1,g2)
    c: Coincident(g2,g3)
    c: Coincident(g3,g4)
    c: Coincident(g4,g5)
    c: Coincident(g5,g0)
    c: Equal(g0, g1-g5) x5
    c: PointOnObject(g0,g6)
    c: PointOnObject(g1,g6)
    c: PointOnObject(g2,g6)
    c: PointOnObject(g3,g6)
    c: PointOnObject(g4,g6)
    c: PointOnObject(g5,g6)
    c: Coincident(g6,g-1)
    c: PointOnObject(g5,g-2)
    c: Radius(g6) = 10.5
    c: Coincident(g7,g0)
    c: Coincident(g8,g4)
    c: Coincident(g9,g3)
    c: Coincident(g10,g2)
    c: Coincident(g11,g1)
    c: Coincident(g12,g0)
    c: Radius(g12) = 0.95
    c: Equal(g12, g7-g11) x5
FEATURE [PartDesign::Pocket] Pocket720  label="Screwholes Servohorn003"
  BaseFeature = -> Fillet240
  Length = 3
  Length2 = 100
  Profile = -> Sketch1937
  Type = 0
FEATURE [Sketcher::SketchObject] Sketch1926
  MapMode = 5
  Placement = pos=(0,0,0) rot=(1,0,0;3.14159rad)
  Support = -> [Pocket720]
  sketch-geometry (10):
    g0: Circle [constr] CenterX=0 CenterY=0 CenterZ=0 NormalX=0 NormalY=0 NormalZ=1 AngleXU=0 Radius=20
    g1: LineSegment [constr] StartX=-14.1421 StartY=14.1421 StartZ=0 EndX=14.1421 EndY=14.1421 EndZ=0
    g2: LineSegment [constr] StartX=14.1421 StartY=14.1421 StartZ=0 EndX=14.1421 EndY=-14.1421 EndZ=0
    g3: LineSegment [constr] StartX=14.1421 StartY=-14.1421 StartZ=0 EndX=-14.1421 EndY=-14.1421 EndZ=0
    g4: LineSegment [constr] StartX=-14.1421 StartY=-14.1421 StartZ=0 EndX=-14.1421 EndY=14.1421 EndZ=0
    g5: Circle CenterX=-14.1421 CenterY=14.1421 CenterZ=0 NormalX=0 NormalY=0 NormalZ=1 AngleXU=0 Radius=1.2e-15
    g6: Circle CenterX=14.1421 CenterY=14.1421 CenterZ=0 NormalX=0 NormalY=0 NormalZ=1 AngleXU=0 Radius=2.85
    g7: Circle CenterX=14.1421 CenterY=-14.1421 CenterZ=0 NormalX=0 NormalY=0 NormalZ=1 AngleXU=0 Radius=2.85
    g8: Circle CenterX=-14.1421 CenterY=14.1421 CenterZ=0 NormalX=0 NormalY=0 NormalZ=1 AngleXU=0 Radius=2.85
    g9: Circle CenterX=-14.1421 CenterY=-14.1421 CenterZ=0 NormalX=0 NormalY=0 NormalZ=1 AngleXU=0 Radius=2.85
  constraints (24):
    c: Coincident(g0,g-1)
    c: Radius(g0) = 20
    c: Coincident(g1,g2)
    c: Coincident(g2,g3)
    c: Coincident(g3,g4)
    c: Coincident(g4,g1)
    c: Horizontal(g1)
    c: Horizontal(g3)
    c: Vertical(g2)
    c: Vertical(g4)
    c: PointOnObject(g1,g0)
    c: PointOnObject(g2,g0)
    c: PointOnObject(g1,g0)
    c: Equal(g1,g2)
    c: Coincident(g5,g1)
    c: Tangent(g5,g0)
    c: Coincident(g6,g1)
    c: Coincident(g7,g2)
    c: Coincident(g8,g5)
    c: Coincident(g9,g3)
    c: Equal(g9,g8)
    c: Equal(g8,g6)
    c: Equal(g6,g7)
    c: Radius(g6) = 2.85
FEATURE [PartDesign::Pocket] Pocket727  label="Screwheads Mounting003"
  BaseFeature = -> Pocket720
  Length = 8
  Length2 = 100
  Profile = -> Sketch1926
  Type = 0
FEATURE [PartDesign::Chamfer] Chamfer394  label="Screwheads Bottom Chamfer003"
  Base = -> Pocket727 [Edge140,Edge139,Edge138,Edge137]
  BaseFeature = -> Pocket727
  Size = 1.2
FEATURE [PartDesign::Body] Body541  label="Shoulder_Joint_Servohorn_Cap003"
  Group = -> [Sketch1915,Pad867,Sketch1925,Pocket724,Sketch1936,Pocket734,Sketch1914,Pocket729,Sketch1932,Pocket725,Fillet240,Sketch1937,Pocket720,Sketch1926,Pocket727,Chamfer394]
  Origin = -> Origin742
  Tip = -> Chamfer394
FEATURE [Sketcher::SketchObject] Sketch1938
  MapMode = 5
  Placement = pos=(0,0,0) rot=(1,0,0;3.14159rad)
  Support = -> [Pocket706]
  sketch-geometry (2):
    g0: Circle CenterX=0 CenterY=0 CenterZ=0 NormalX=0 NormalY=0 NormalZ=1 AngleXU=0 Radius=4.5
    g1: Circle CenterX=0 CenterY=0 CenterZ=0 NormalX=0 NormalY=0 NormalZ=1 AngleXU=0 Radius=3
  constraints (4):
    c: Coincident(g0,g-1)
    c: Coincident(g1,g0)
    c: Radius(g0) = 4.5
    c: Radius(g1) = 3
FEATURE [PartDesign::Pad] Pad843
  BaseFeature = -> Pocket706
  Length = 3
  Length2 = 100
  Profile = -> Sketch1938
  Type = 0
FEATURE [PartDesign::Fillet] Fillet242
  Base = -> Pad843 [Face5,Edge96,Face4]
  BaseFeature = -> Pad843
  Radius = 0.2
FEATURE [Sketcher::SketchObject] Sketch1939
  MapMode = 5
  Support = -> [XY_Plane775]
  sketch-geometry (1):
    g0: Circle CenterX=0 CenterY=0 CenterZ=0 NormalX=0 NormalY=0 NormalZ=1 AngleXU=0 Radius=1.9
  constraints (2):
    c: Coincident(g0,g-1)
    c: Radius(g0) = 1.9
FEATURE [PartDesign::Pad] Pad841  label="M3x8 Head106"
  Length = 2
  Length2 = 100
  Profile = -> Sketch1939
  Type = 0
FEATURE [Sketcher::SketchObject] Sketch1940
  MapMode = 5
  Placement = pos=(0,0,2) rot=(0,0,1;0rad)
  Support = -> [Pad835]
  sketch-geometry (1):
    g0: Circle CenterX=0 CenterY=0 CenterZ=0 NormalX=0 NormalY=0 NormalZ=1 AngleXU=0 Radius=1
  constraints (2):
    c: Coincident(g0,g-1)
    c: Radius(g0) = 1
FEATURE [PartDesign::Pad] Pad856  label="M3x8 Thread108"
  BaseFeature = -> Pad835
  Length = 8
  Length2 = 100
  Profile = -> Sketch1940
  Type = 0
FEATURE [Sketcher::SketchObject] Sketch1928
  MapMode = 5
  Placement = pos=(0,0,0) rot=(1,0,0;3.14159rad)
  Support = -> [Pad856]
  sketch-geometry (7):
    g0: LineSegment StartX=0.77 StartY=0.44456 StartZ=0 EndX=0 EndY=0.889119 EndZ=0
    g1: LineSegment StartX=0 StartY=0.889119 StartZ=0 EndX=-0.77 EndY=0.44456 EndZ=0
    g2: LineSegment StartX=-0.77 StartY=0.44456 StartZ=0 EndX=-0.77 EndY=-0.44456 EndZ=0
    g3: LineSegment StartX=-0.77 StartY=-0.44456 StartZ=0 EndX=3.85628e-11 EndY=-0.889119 EndZ=0
    g4: LineSegment StartX=3.85628e-11 StartY=-0.889119 StartZ=0 EndX=0.77 EndY=-0.44456 EndZ=0
    g5: LineSegment StartX=0.77 StartY=-0.44456 StartZ=0 EndX=0.77 EndY=0.44456 EndZ=0
    g6: Circle [constr] CenterX=0 CenterY=0 CenterZ=0 NormalX=0 NormalY=0 NormalZ=1 AngleXU=0 Radius=0.889119
  constraints (16):
    c: Coincident(g0,g1)
    c: Coincident(g1,g2)
    c: Coincident(g2,g3)
    c: Coincident(g3,g4)
    c: Coincident(g4,g5)
    c: Coincident(g5,g0)
    c: Equal(g0, g1-g5) x5
    c: PointOnObject(g0,g6)
    c: PointOnObject(g1,g6)
    c: PointOnObject(g2,g6)
    c: PointOnObject(g3,g6)
    c: PointOnObject(g4,g6)
    c: PointOnObject(g5,g6)
    c: Coincident(g6,g-1)
    c: PointOnObject(g0,g-2)
    c: DistanceX(g1,g0) = 1.54
FEATURE [PartDesign::Pocket] Pocket712  label="M3x8 Wrench103"
  BaseFeature = -> Pad856
  Length = 1
  Length2 = 100
  Profile = -> Sketch1928
  Type = 0
FEATURE [PartDesign::Chamfer] Chamfer393  label="M3x8 Smooth102"
  Base = -> Pocket712 [Face11,Edge2,Edge24,Edge3]
  BaseFeature = -> Pocket712
  Size = 0.2
FEATURE [PartDesign::Body] Body536  label="M2x076"
  Group = -> [Sketch1930,Pad835,Sketch1940,Pad856,Sketch1928,Pocket712,Chamfer393]
  Origin = -> Origin759
  Tip = -> Chamfer393
FEATURE [Sketcher::SketchObject] Sketch1943
  MapMode = 5
  Support = -> [XY_Plane739]
  sketch-geometry (8):
    g0: LineSegment StartX=0 StartY=2.3094 StartZ=0 EndX=-2 EndY=1.1547 EndZ=0
    g1: LineSegment StartX=-2 StartY=1.1547 StartZ=0 EndX=-2 EndY=-1.1547 EndZ=0
    g2: LineSegment StartX=-2 StartY=-1.1547 StartZ=0 EndX=-2e-16 EndY=-2.3094 EndZ=0
    g3: LineSegment StartX=-2e-16 StartY=-2.3094 StartZ=0 EndX=2 EndY=-1.1547 EndZ=0
    g4: LineSegment StartX=2 StartY=-1.1547 StartZ=0 EndX=2 EndY=1.1547 EndZ=0
    g5: LineSegment StartX=2 StartY=1.1547 StartZ=0 EndX=0 EndY=2.3094 EndZ=0
    g6: Circle [constr] CenterX=0 CenterY=0 CenterZ=0 NormalX=0 NormalY=0 NormalZ=1 AngleXU=0 Radius=2.3094
    g7: Circle CenterX=0 CenterY=0 CenterZ=0 NormalX=0 NormalY=0 NormalZ=1 AngleXU=0 Radius=1
  constraints (18):
    c: Coincident(g0,g1)
    c: Coincident(g1,g2)
    c: Coincident(g2,g3)
    c: Coincident(g3,g4)
    c: Coincident(g4,g5)
    c: Coincident(g5,g0)
    c: Equal(g0, g1-g5) x5
    c: PointOnObject(g0,g6)
    c: PointOnObject(g1,g6)
    c: PointOnObject(g2,g6)
    c: PointOnObject(g3,g6)
    c: PointOnObject(g4,g6)
    c: PointOnObject(g5,g6)
    c: Coincident(g6,g-1)
    c: PointOnObject(g5,g-2)
    c: DistanceX(g0,g4) = 4
    c: Coincident(g7,g-1)
    c: Radius(g7) = 1
FEATURE [PartDesign::Pad] Pad847  label="M3 Nut Primitive166"
  Length = 0.6
  Length2 = 0.6
  Profile = -> Sketch1943
  Type = 4
FEATURE [Sketcher::SketchObject] Sketch1942
  ExternalGeometry = -> [Pad847]
  MapMode = 5
  Placement = pos=(0,0,0) rot=(0.57735,0.57735,0.57735;2.0944rad)
  Support = -> [YZ_Plane749]
  sketch-geometry (6):
    g0: LineSegment StartX=-1.9594 StartY=0.6 StartZ=0 EndX=-2.8094 EndY=0.6 EndZ=0
    g1: LineSegment StartX=-2.8094 StartY=0.6 StartZ=0 EndX=-2.8094 EndY=-0.6 EndZ=0
    g2: LineSegment StartX=-2.8094 StartY=-0.6 StartZ=0 EndX=-1.9594 EndY=-0.6 EndZ=0
    g3: LineSegment StartX=-1.9594 StartY=-0.6 StartZ=0 EndX=-2.3094 EndY=-0.4 EndZ=0
    g4: LineSegment StartX=-2.3094 StartY=-0.4 StartZ=0 EndX=-2.3094 EndY=0.4 EndZ=0
    g5: LineSegment StartX=-2.3094 StartY=0.4 StartZ=0 EndX=-1.9594 EndY=0.6 EndZ=0
  constraints (15):
    c: Horizontal(g0)
    c: Coincident(g0,g1)
    c: Coincident(g1,g2)
    c: Coincident(g2,g3)
    c: Coincident(g3,g4)
    c: Coincident(g4,g5)
    c: Coincident(g5,g0)
    c: Symmetric(g4,g3,g-1)
    c: Symmetric(g0,g2,g-1)
    c: Symmetric(g1,g0,g-1)
    c: DistanceX(g0,g4) = 0.5
    c: DistanceY(g3,g4) = 0.8
    c: DistanceY(g1,g0) = 1.2
    c: PointOnObject(g3,g-3)
    c: DistanceX(g4,g0) = 0.35
FEATURE [PartDesign::Groove] Groove178  label="M3 Nut Smooth170"
  Angle = 360
  Axis = (-2e-16,3e-16,1)
  Base = (0,0,0)
  BaseFeature = -> Pad847
  Profile = -> Sketch1942
  ReferenceAxis = -> Sketch1942 [V_Axis]
  Reversed = true
FEATURE [PartDesign::Chamfer] Chamfer407  label="M3 Nut Smooth Hole171"
  Base = -> Groove178 [Edge24,Edge23]
  BaseFeature = -> Groove178
  Size = 0.2
FEATURE [PartDesign::Body] Body549  label="M2 Nut067"
  Group = -> [Sketch1943,Pad847,Sketch1942,Groove178,Chamfer407,Sketch1933,Sketch1927]
  Origin = -> Origin744
  Placement = pos=(0,0,2.75) rot=(0,0,1;0rad)
  Tip = -> Chamfer407
FEATURE [Sketcher::SketchObject] Sketch1946
  MapMode = 5
  Support = -> [XY_Plane745]
FEATURE [Sketcher::SketchObject] Sketch1950
  MapMode = 5
  Placement = pos=(0,0,2) rot=(0,0,1;0rad)
  Support = -> [Pad841]
  sketch-geometry (1):
    g0: Circle CenterX=0 CenterY=0 CenterZ=0 NormalX=0 NormalY=0 NormalZ=1 AngleXU=0 Radius=1
  constraints (2):
    c: Coincident(g0,g-1)
    c: Radius(g0) = 1
FEATURE [PartDesign::Pad] Pad832  label="M3x8 Thread102"
  BaseFeature = -> Pad841
  Length = 8
  Length2 = 100
  Profile = -> Sketch1950
  Type = 0
FEATURE [Sketcher::SketchObject] Sketch1945
  MapMode = 5
  Placement = pos=(0,0,0) rot=(1,0,0;3.14159rad)
  Support = -> [Pad832]
  sketch-geometry (7):
    g0: LineSegment StartX=0.77 StartY=0.44456 StartZ=0 EndX=0 EndY=0.889119 EndZ=0
    g1: LineSegment StartX=0 StartY=0.889119 StartZ=0 EndX=-0.77 EndY=0.44456 EndZ=0
    g2: LineSegment StartX=-0.77 StartY=0.44456 StartZ=0 EndX=-0.77 EndY=-0.44456 EndZ=0
    g3: LineSegment StartX=-0.77 StartY=-0.44456 StartZ=0 EndX=3.85628e-11 EndY=-0.889119 EndZ=0
    g4: LineSegment StartX=3.85628e-11 StartY=-0.889119 StartZ=0 EndX=0.77 EndY=-0.44456 EndZ=0
    g5: LineSegment StartX=0.77 StartY=-0.44456 StartZ=0 EndX=0.77 EndY=0.44456 EndZ=0
    g6: Circle [constr] CenterX=0 CenterY=0 CenterZ=0 NormalX=0 NormalY=0 NormalZ=1 AngleXU=0 Radius=0.889119
  constraints (16):
    c: Coincident(g0,g1)
    c: Coincident(g1,g2)
    c: Coincident(g2,g3)
    c: Coincident(g3,g4)
    c: Coincident(g4,g5)
    c: Coincident(g5,g0)
    c: Equal(g0, g1-g5) x5
    c: PointOnObject(g0,g6)
    c: PointOnObject(g1,g6)
    c: PointOnObject(g2,g6)
    c: PointOnObject(g3,g6)
    c: PointOnObject(g4,g6)
    c: PointOnObject(g5,g6)
    c: Coincident(g6,g-1)
    c: PointOnObject(g0,g-2)
    c: DistanceX(g1,g0) = 1.54
FEATURE [PartDesign::Pocket] Pocket714  label="M3x8 Wrench105"
  BaseFeature = -> Pad832
  Length = 1
  Length2 = 100
  Profile = -> Sketch1945
  Type = 0
FEATURE [PartDesign::Chamfer] Chamfer397  label="M3x8 Smooth104"
  Base = -> Pocket714 [Face11,Edge2,Edge24,Edge3]
  BaseFeature = -> Pocket714
  Size = 0.2
FEATURE [PartDesign::Body] Body548  label="M2x078"
  Group = -> [Sketch1939,Pad841,Sketch1950,Pad832,Sketch1945,Pocket714,Chamfer397]
  Origin = -> Origin767
  Tip = -> Chamfer397
FEATURE [App::Part] Part206  label="M062"
  Group = -> [Body548,Body549]
  Origin = -> Origin771
  Placement = pos=(-9.1,-5.25,80) rot=(0,1,0;3.14159rad)
FEATURE [Sketcher::SketchObject] Sketch1951
  MapMode = 5
  Support = -> [XY_Plane745]
  sketch-geometry (8):
    g0: LineSegment StartX=0 StartY=2.3094 StartZ=0 EndX=-2 EndY=1.1547 EndZ=0
    g1: LineSegment StartX=-2 StartY=1.1547 StartZ=0 EndX=-2 EndY=-1.1547 EndZ=0
    g2: LineSegment StartX=-2 StartY=-1.1547 StartZ=0 EndX=-2e-16 EndY=-2.3094 EndZ=0
    g3: LineSegment StartX=-2e-16 StartY=-2.3094 StartZ=0 EndX=2 EndY=-1.1547 EndZ=0
    g4: LineSegment StartX=2 StartY=-1.1547 StartZ=0 EndX=2 EndY=1.1547 EndZ=0
    g5: LineSegment StartX=2 StartY=1.1547 StartZ=0 EndX=0 EndY=2.3094 EndZ=0
    g6: Circle [constr] CenterX=0 CenterY=0 CenterZ=0 NormalX=0 NormalY=0 NormalZ=1 AngleXU=0 Radius=2.3094
    g7: Circle CenterX=0 CenterY=0 CenterZ=0 NormalX=0 NormalY=0 NormalZ=1 AngleXU=0 Radius=1
  constraints (18):
    c: Coincident(g0,g1)
    c: Coincident(g1,g2)
    c: Coincident(g2,g3)
    c: Coincident(g3,g4)
    c: Coincident(g4,g5)
    c: Coincident(g5,g0)
    c: Equal(g0, g1-g5) x5
    c: PointOnObject(g0,g6)
    c: PointOnObject(g1,g6)
    c: PointOnObject(g2,g6)
    c: PointOnObject(g3,g6)
    c: PointOnObject(g4,g6)
    c: PointOnObject(g5,g6)
    c: Coincident(g6,g-1)
    c: PointOnObject(g5,g-2)
    c: DistanceX(g0,g4) = 4
    c: Coincident(g7,g-1)
    c: Radius(g7) = 1
FEATURE [PartDesign::Pad] Pad842  label="M3 Nut Primitive164"
  Length = 0.6
  Length2 = 0.6
  Profile = -> Sketch1951
  Type = 4
FEATURE [Sketcher::SketchObject] Sketch1908
  ExternalGeometry = -> [Pad842]
  MapMode = 5
  Placement = pos=(0,0,0) rot=(0.57735,0.57735,0.57735;2.0944rad)
  Support = -> [YZ_Plane737]
  sketch-geometry (6):
    g0: LineSegment StartX=-1.9594 StartY=0.6 StartZ=0 EndX=-2.8094 EndY=0.6 EndZ=0
    g1: LineSegment StartX=-2.8094 StartY=0.6 StartZ=0 EndX=-2.8094 EndY=-0.6 EndZ=0
    g2: LineSegment StartX=-2.8094 StartY=-0.6 StartZ=0 EndX=-1.9594 EndY=-0.6 EndZ=0
    g3: LineSegment StartX=-1.9594 StartY=-0.6 StartZ=0 EndX=-2.3094 EndY=-0.4 EndZ=0
    g4: LineSegment StartX=-2.3094 StartY=-0.4 StartZ=0 EndX=-2.3094 EndY=0.4 EndZ=0
    g5: LineSegment StartX=-2.3094 StartY=0.4 StartZ=0 EndX=-1.9594 EndY=0.6 EndZ=0
  constraints (15):
    c: Horizontal(g0)
    c: Coincident(g0,g1)
    c: Coincident(g1,g2)
    c: Coincident(g2,g3)
    c: Coincident(g3,g4)
    c: Coincident(g4,g5)
    c: Coincident(g5,g0)
    c: Symmetric(g4,g3,g-1)
    c: Symmetric(g0,g2,g-1)
    c: Symmetric(g1,g0,g-1)
    c: DistanceX(g0,g4) = 0.5
    c: DistanceY(g3,g4) = 0.8
    c: DistanceY(g1,g0) = 1.2
    c: PointOnObject(g3,g-3)
    c: DistanceX(g4,g0) = 0.35
FEATURE [PartDesign::Groove] Groove172  label="M3 Nut Smooth164"
  Angle = 360
  Axis = (-2e-16,3e-16,1)
  Base = (0,0,0)
  BaseFeature = -> Pad842
  Profile = -> Sketch1908
  ReferenceAxis = -> Sketch1908 [V_Axis]
  Reversed = true
FEATURE [PartDesign::Chamfer] Chamfer413  label="M3 Nut Smooth Hole174"
  Base = -> Groove172 [Edge24,Edge23]
  BaseFeature = -> Groove172
  Size = 0.2
FEATURE [PartDesign::Body] Body552  label="M2 Nut069"
  Group = -> [Sketch1951,Pad842,Sketch1908,Groove172,Chamfer413,Sketch1929,Sketch1946]
  Origin = -> Origin738
  Placement = pos=(0,0,2.75) rot=(0,0,1;0rad)
  Tip = -> Chamfer413
FEATURE [Sketcher::SketchObject] Sketch1952
  MapMode = 5
  Placement = pos=(0,0,2) rot=(0,0,1;0rad)
  Support = -> [Pad840]
  sketch-geometry (1):
    g0: Circle CenterX=0 CenterY=0 CenterZ=0 NormalX=0 NormalY=0 NormalZ=1 AngleXU=0 Radius=1
  constraints (2):
    c: Coincident(g0,g-1)
    c: Radius(g0) = 1
FEATURE [PartDesign::Pad] Pad839  label="M3x8 Thread104"
  BaseFeature = -> Pad840
  Length = 8
  Length2 = 100
  Profile = -> Sketch1952
  Type = 0
FEATURE [Sketcher::SketchObject] Sketch1947
  MapMode = 5
  Placement = pos=(0,0,0) rot=(1,0,0;3.14159rad)
  Support = -> [Pad839]
  sketch-geometry (7):
    g0: LineSegment StartX=0.77 StartY=0.44456 StartZ=0 EndX=0 EndY=0.889119 EndZ=0
    g1: LineSegment StartX=0 StartY=0.889119 StartZ=0 EndX=-0.77 EndY=0.44456 EndZ=0
    g2: LineSegment StartX=-0.77 StartY=0.44456 StartZ=0 EndX=-0.77 EndY=-0.44456 EndZ=0
    g3: LineSegment StartX=-0.77 StartY=-0.44456 StartZ=0 EndX=3.85628e-11 EndY=-0.889119 EndZ=0
    g4: LineSegment StartX=3.85628e-11 StartY=-0.889119 StartZ=0 EndX=0.77 EndY=-0.44456 EndZ=0
    g5: LineSegment StartX=0.77 StartY=-0.44456 StartZ=0 EndX=0.77 EndY=0.44456 EndZ=0
    g6: Circle [constr] CenterX=0 CenterY=0 CenterZ=0 NormalX=0 NormalY=0 NormalZ=1 AngleXU=0 Radius=0.889119
  constraints (16):
    c: Coincident(g0,g1)
    c: Coincident(g1,g2)
    c: Coincident(g2,g3)
    c: Coincident(g3,g4)
    c: Coincident(g4,g5)
    c: Coincident(g5,g0)
    c: Equal(g0, g1-g5) x5
    c: PointOnObject(g0,g6)
    c: PointOnObject(g1,g6)
    c: PointOnObject(g2,g6)
    c: PointOnObject(g3,g6)
    c: PointOnObject(g4,g6)
    c: PointOnObject(g5,g6)
    c: Coincident(g6,g-1)
    c: PointOnObject(g0,g-2)
    c: DistanceX(g1,g0) = 1.54
FEATURE [PartDesign::Pocket] Pocket713  label="M3x8 Wrench104"
  BaseFeature = -> Pad839
  Length = 1
  Length2 = 100
  Profile = -> Sketch1947
  Type = 0
FEATURE [PartDesign::Chamfer] Chamfer398  label="M3x8 Smooth105"
  Base = -> Pocket713 [Face11,Edge2,Edge24,Edge3]
  BaseFeature = -> Pocket713
  Size = 0.2
FEATURE [PartDesign::Body] Body554  label="M2x080"
  Group = -> [Sketch1935,Pad840,Sketch1952,Pad839,Sketch1947,Pocket713,Chamfer398]
  Origin = -> Origin777
  Tip = -> Chamfer398
FEATURE [App::Part] Part214  label="M065"
  Group = -> [Body554,Body552]
  Origin = -> Origin749
  Placement = pos=(-9.8e-15,-10.5,80) rot=(0,1,0;3.14159rad)
FEATURE [Sketcher::SketchObject] Sketch1953
  MapMode = 5
  Support = -> [XY_Plane770]
FEATURE [Sketcher::SketchObject] Sketch1955
  MapMode = 5
  Support = -> [XY_Plane774]
  sketch-geometry (1):
    g0: Circle CenterX=0 CenterY=0 CenterZ=0 NormalX=0 NormalY=0 NormalZ=1 AngleXU=0 Radius=1.9
  constraints (2):
    c: Coincident(g0,g-1)
    c: Radius(g0) = 1.9
FEATURE [PartDesign::Pad] Pad836  label="M3x8 Head103"
  Length = 2
  Length2 = 100
  Profile = -> Sketch1955
  Type = 0
FEATURE [Sketcher::SketchObject] Sketch1949
  MapMode = 5
  Placement = pos=(0,0,2) rot=(0,0,1;0rad)
  Support = -> [Pad836]
  sketch-geometry (1):
    g0: Circle CenterX=0 CenterY=0 CenterZ=0 NormalX=0 NormalY=0 NormalZ=1 AngleXU=0 Radius=1
  constraints (2):
    c: Coincident(g0,g-1)
    c: Radius(g0) = 1
FEATURE [PartDesign::Pad] Pad857  label="M3x8 Thread109"
  BaseFeature = -> Pad836
  Length = 8
  Length2 = 100
  Profile = -> Sketch1949
  Type = 0
FEATURE [Sketcher::SketchObject] Sketch1956
  MapMode = 5
  Support = -> [XY_Plane759]
FEATURE [Sketcher::SketchObject] Sketch1957
  MapMode = 5
  Support = -> [XY_Plane738]
FEATURE [Sketcher::SketchObject] Sketch1958
  MapMode = 5
  Support = -> [XY_Plane760]
  sketch-geometry (1):
    g0: Circle CenterX=0 CenterY=0 CenterZ=0 NormalX=0 NormalY=0 NormalZ=1 AngleXU=0 Radius=1.9
  constraints (2):
    c: Coincident(g0,g-1)
    c: Radius(g0) = 1.9
FEATURE [PartDesign::Pad] Pad852  label="M3x8 Head108"
  Length = 2
  Length2 = 100
  Profile = -> Sketch1958
  Type = 0
FEATURE [Sketcher::SketchObject] Sketch1944
  MapMode = 5
  Placement = pos=(0,0,2) rot=(0,0,1;0rad)
  Support = -> [Pad852]
  sketch-geometry (1):
    g0: Circle CenterX=0 CenterY=0 CenterZ=0 NormalX=0 NormalY=0 NormalZ=1 AngleXU=0 Radius=1
  constraints (2):
    c: Coincident(g0,g-1)
    c: Radius(g0) = 1
FEATURE [PartDesign::Pad] Pad846  label="M3x8 Thread105"
  BaseFeature = -> Pad852
  Length = 8
  Length2 = 100
  Profile = -> Sketch1944
  Type = 0
FEATURE [Sketcher::SketchObject] Sketch1948
  MapMode = 5
  Placement = pos=(0,0,0) rot=(1,0,0;3.14159rad)
  Support = -> [Pad846]
  sketch-geometry (7):
    g0: LineSegment StartX=0.77 StartY=0.44456 StartZ=0 EndX=0 EndY=0.889119 EndZ=0
    g1: LineSegment StartX=0 StartY=0.889119 StartZ=0 EndX=-0.77 EndY=0.44456 EndZ=0
    g2: LineSegment StartX=-0.77 StartY=0.44456 StartZ=0 EndX=-0.77 EndY=-0.44456 EndZ=0
    g3: LineSegment StartX=-0.77 StartY=-0.44456 StartZ=0 EndX=3.85628e-11 EndY=-0.889119 EndZ=0
    g4: LineSegment StartX=3.85628e-11 StartY=-0.889119 StartZ=0 EndX=0.77 EndY=-0.44456 EndZ=0
    g5: LineSegment StartX=0.77 StartY=-0.44456 StartZ=0 EndX=0.77 EndY=0.44456 EndZ=0
    g6: Circle [constr] CenterX=0 CenterY=0 CenterZ=0 NormalX=0 NormalY=0 NormalZ=1 AngleXU=0 Radius=0.889119
  constraints (16):
    c: Coincident(g0,g1)
    c: Coincident(g1,g2)
    c: Coincident(g2,g3)
    c: Coincident(g3,g4)
    c: Coincident(g4,g5)
    c: Coincident(g5,g0)
    c: Equal(g0, g1-g5) x5
    c: PointOnObject(g0,g6)
    c: PointOnObject(g1,g6)
    c: PointOnObject(g2,g6)
    c: PointOnObject(g3,g6)
    c: PointOnObject(g4,g6)
    c: PointOnObject(g5,g6)
    c: Coincident(g6,g-1)
    c: PointOnObject(g0,g-2)
    c: DistanceX(g1,g0) = 1.54
FEATURE [PartDesign::Pocket] Pocket716  label="M3x8 Wrench107"
  BaseFeature = -> Pad846
  Length = 1
  Length2 = 100
  Profile = -> Sketch1948
  Type = 0
FEATURE [PartDesign::Chamfer] Chamfer399  label="M3x8 Smooth106"
  Base = -> Pocket716 [Face11,Edge2,Edge24,Edge3]
  BaseFeature = -> Pocket716
  Size = 0.2
FEATURE [PartDesign::Body] Body546  label="M2x077"
  Group = -> [Sketch1958,Pad852,Sketch1944,Pad846,Sketch1948,Pocket716,Chamfer399]
  Origin = -> Origin741
  Tip = -> Chamfer399
FEATURE [Sketcher::SketchObject] Sketch1959
  MapMode = 5
  Support = -> [XY_Plane759]
FEATURE [Sketcher::SketchObject] Sketch1960
  MapMode = 5
  Placement = pos=(0,0,0) rot=(1,0,0;3.14159rad)
  Support = -> [Pad857]
  sketch-geometry (7):
    g0: LineSegment StartX=0.77 StartY=0.44456 StartZ=0 EndX=0 EndY=0.889119 EndZ=0
    g1: LineSegment StartX=0 StartY=0.889119 StartZ=0 EndX=-0.77 EndY=0.44456 EndZ=0
    g2: LineSegment StartX=-0.77 StartY=0.44456 StartZ=0 EndX=-0.77 EndY=-0.44456 EndZ=0
    g3: LineSegment StartX=-0.77 StartY=-0.44456 StartZ=0 EndX=3.85628e-11 EndY=-0.889119 EndZ=0
    g4: LineSegment StartX=3.85628e-11 StartY=-0.889119 StartZ=0 EndX=0.77 EndY=-0.44456 EndZ=0
    g5: LineSegment StartX=0.77 StartY=-0.44456 StartZ=0 EndX=0.77 EndY=0.44456 EndZ=0
    g6: Circle [constr] CenterX=0 CenterY=0 CenterZ=0 NormalX=0 NormalY=0 NormalZ=1 AngleXU=0 Radius=0.889119
  constraints (16):
    c: Coincident(g0,g1)
    c: Coincident(g1,g2)
    c: Coincident(g2,g3)
    c: Coincident(g3,g4)
    c: Coincident(g4,g5)
    c: Coincident(g5,g0)
    c: Equal(g0, g1-g5) x5
    c: PointOnObject(g0,g6)
    c: PointOnObject(g1,g6)
    c: PointOnObject(g2,g6)
    c: PointOnObject(g3,g6)
    c: PointOnObject(g4,g6)
    c: PointOnObject(g5,g6)
    c: Coincident(g6,g-1)
    c: PointOnObject(g0,g-2)
    c: DistanceX(g1,g0) = 1.54
FEATURE [PartDesign::Pocket] Pocket718  label="M3x8 Wrench109"
  BaseFeature = -> Pad857
  Length = 1
  Length2 = 100
  Profile = -> Sketch1960
  Type = 0
FEATURE [PartDesign::Chamfer] Chamfer403  label="M3x8 Smooth107"
  Base = -> Pocket718 [Face11,Edge2,Edge24,Edge3]
  BaseFeature = -> Pocket718
  Size = 0.2
FEATURE [PartDesign::Body] Body534  label="M2x074"
  Group = -> [Sketch1955,Pad836,Sketch1949,Pad857,Sketch1960,Pocket718,Chamfer403]
  Origin = -> Origin746
  Tip = -> Chamfer403
FEATURE [Sketcher::SketchObject] Sketch1961
  MapMode = 5
  Support = -> [XY_Plane770]
FEATURE [Sketcher::SketchObject] Sketch1963
  MapMode = 5
  Support = -> [XY_Plane759]
  sketch-geometry (8):
    g0: LineSegment StartX=0 StartY=2.3094 StartZ=0 EndX=-2 EndY=1.1547 EndZ=0
    g1: LineSegment StartX=-2 StartY=1.1547 StartZ=0 EndX=-2 EndY=-1.1547 EndZ=0
    g2: LineSegment StartX=-2 StartY=-1.1547 StartZ=0 EndX=-2e-16 EndY=-2.3094 EndZ=0
    g3: LineSegment StartX=-2e-16 StartY=-2.3094 StartZ=0 EndX=2 EndY=-1.1547 EndZ=0
    g4: LineSegment StartX=2 StartY=-1.1547 StartZ=0 EndX=2 EndY=1.1547 EndZ=0
    g5: LineSegment StartX=2 StartY=1.1547 StartZ=0 EndX=0 EndY=2.3094 EndZ=0
    g6: Circle [constr] CenterX=0 CenterY=0 CenterZ=0 NormalX=0 NormalY=0 NormalZ=1 AngleXU=0 Radius=2.3094
    g7: Circle CenterX=0 CenterY=0 CenterZ=0 NormalX=0 NormalY=0 NormalZ=1 AngleXU=0 Radius=1
  constraints (18):
    c: Coincident(g0,g1)
    c: Coincident(g1,g2)
    c: Coincident(g2,g3)
    c: Coincident(g3,g4)
    c: Coincident(g4,g5)
    c: Coincident(g5,g0)
    c: Equal(g0, g1-g5) x5
    c: PointOnObject(g0,g6)
    c: PointOnObject(g1,g6)
    c: PointOnObject(g2,g6)
    c: PointOnObject(g3,g6)
    c: PointOnObject(g4,g6)
    c: PointOnObject(g5,g6)
    c: Coincident(g6,g-1)
    c: PointOnObject(g5,g-2)
    c: DistanceX(g0,g4) = 4
    c: Coincident(g7,g-1)
    c: Radius(g7) = 1
FEATURE [PartDesign::Pad] Pad854  label="M3 Nut Primitive168"
  Length = 0.6
  Length2 = 0.6
  Profile = -> Sketch1963
  Type = 4
FEATURE [Sketcher::SketchObject] Sketch1941
  ExternalGeometry = -> [Pad854]
  MapMode = 5
  Placement = pos=(0,0,0) rot=(0.57735,0.57735,0.57735;2.0944rad)
  Support = -> [YZ_Plane757]
  sketch-geometry (6):
    g0: LineSegment StartX=-1.9594 StartY=0.6 StartZ=0 EndX=-2.8094 EndY=0.6 EndZ=0
    g1: LineSegment StartX=-2.8094 StartY=0.6 StartZ=0 EndX=-2.8094 EndY=-0.6 EndZ=0
    g2: LineSegment StartX=-2.8094 StartY=-0.6 StartZ=0 EndX=-1.9594 EndY=-0.6 EndZ=0
    g3: LineSegment StartX=-1.9594 StartY=-0.6 StartZ=0 EndX=-2.3094 EndY=-0.4 EndZ=0
    g4: LineSegment StartX=-2.3094 StartY=-0.4 StartZ=0 EndX=-2.3094 EndY=0.4 EndZ=0
    g5: LineSegment StartX=-2.3094 StartY=0.4 StartZ=0 EndX=-1.9594 EndY=0.6 EndZ=0
  constraints (15):
    c: Horizontal(g0)
    c: Coincident(g0,g1)
    c: Coincident(g1,g2)
    c: Coincident(g2,g3)
    c: Coincident(g3,g4)
    c: Coincident(g4,g5)
    c: Coincident(g5,g0)
    c: Symmetric(g4,g3,g-1)
    c: Symmetric(g0,g2,g-1)
    c: Symmetric(g1,g0,g-1)
    c: DistanceX(g0,g4) = 0.5
    c: DistanceY(g3,g4) = 0.8
    c: DistanceY(g1,g0) = 1.2
    c: PointOnObject(g3,g-3)
    c: DistanceX(g4,g0) = 0.35
FEATURE [PartDesign::Groove] Groove175  label="M3 Nut Smooth167"
  Angle = 360
  Axis = (-2e-16,3e-16,1)
  Base = (0,0,0)
  BaseFeature = -> Pad854
  Profile = -> Sketch1941
  ReferenceAxis = -> Sketch1941 [V_Axis]
  Reversed = true
FEATURE [PartDesign::Chamfer] Chamfer405  label="M3 Nut Smooth Hole170"
  Base = -> Groove175 [Edge24,Edge23]
  BaseFeature = -> Groove175
  Size = 0.2
FEATURE [PartDesign::Body] Body547  label="M2 Nut066"
  Group = -> [Sketch1963,Pad854,Sketch1941,Groove175,Chamfer405,Sketch1956,Sketch1959]
  Origin = -> Origin765
  Placement = pos=(0,0,2.75) rot=(0,0,1;0rad)
  Tip = -> Chamfer405
FEATURE [App::Part] Part217  label="M067"
  Group = -> [Body534,Body547]
  Origin = -> Origin752
  Placement = pos=(9.1,5.25,80) rot=(0,1,0;3.14159rad)
FEATURE [Sketcher::SketchObject] Sketch1964
  ExternalGeometry = -> [Pad848]
  MapMode = 5
  Placement = pos=(0,0,0) rot=(0.57735,0.57735,0.57735;2.0944rad)
  Support = -> [YZ_Plane750]
  sketch-geometry (6):
    g0: LineSegment StartX=-1.9594 StartY=0.6 StartZ=0 EndX=-2.8094 EndY=0.6 EndZ=0
    g1: LineSegment StartX=-2.8094 StartY=0.6 StartZ=0 EndX=-2.8094 EndY=-0.6 EndZ=0
    g2: LineSegment StartX=-2.8094 StartY=-0.6 StartZ=0 EndX=-1.9594 EndY=-0.6 EndZ=0
    g3: LineSegment StartX=-1.9594 StartY=-0.6 StartZ=0 EndX=-2.3094 EndY=-0.4 EndZ=0
    g4: LineSegment StartX=-2.3094 StartY=-0.4 StartZ=0 EndX=-2.3094 EndY=0.4 EndZ=0
    g5: LineSegment StartX=-2.3094 StartY=0.4 StartZ=0 EndX=-1.9594 EndY=0.6 EndZ=0
  constraints (15):
    c: Horizontal(g0)
    c: Coincident(g0,g1)
    c: Coincident(g1,g2)
    c: Coincident(g2,g3)
    c: Coincident(g3,g4)
    c: Coincident(g4,g5)
    c: Coincident(g5,g0)
    c: Symmetric(g4,g3,g-1)
    c: Symmetric(g0,g2,g-1)
    c: Symmetric(g1,g0,g-1)
    c: DistanceX(g0,g4) = 0.5
    c: DistanceY(g3,g4) = 0.8
    c: DistanceY(g1,g0) = 1.2
    c: PointOnObject(g3,g-3)
    c: DistanceX(g4,g0) = 0.35
FEATURE [PartDesign::Groove] Groove177  label="M3 Nut Smooth169"
  Angle = 360
  Axis = (-2e-16,3e-16,1)
  Base = (0,0,0)
  BaseFeature = -> Pad848
  Profile = -> Sketch1964
  ReferenceAxis = -> Sketch1964 [V_Axis]
  Reversed = true
FEATURE [PartDesign::Chamfer] Chamfer401  label="M3 Nut Smooth Hole167"
  Base = -> Groove177 [Edge24,Edge23]
  BaseFeature = -> Groove177
  Size = 0.2
FEATURE [PartDesign::Body] Body543  label="M2 Nut065"
  Group = -> [Sketch1909,Pad848,Sketch1964,Groove177,Chamfer401,Sketch1953,Sketch1961]
  Origin = -> Origin751
  Placement = pos=(0,0,2.75) rot=(0,0,1;0rad)
  Tip = -> Chamfer401
FEATURE [App::Part] Part212  label="M064"
  Group = -> [Body546,Body543]
  Origin = -> Origin754
  Placement = pos=(9.1,-5.25,80) rot=(0,1,0;3.14159rad)
FEATURE [Sketcher::SketchObject] Sketch1965
  MapMode = 5
  Support = -> [XY_Plane738]
  sketch-geometry (8):
    g0: LineSegment StartX=0 StartY=2.3094 StartZ=0 EndX=-2 EndY=1.1547 EndZ=0
    g1: LineSegment StartX=-2 StartY=1.1547 StartZ=0 EndX=-2 EndY=-1.1547 EndZ=0
    g2: LineSegment StartX=-2 StartY=-1.1547 StartZ=0 EndX=-2e-16 EndY=-2.3094 EndZ=0
    g3: LineSegment StartX=-2e-16 StartY=-2.3094 StartZ=0 EndX=2 EndY=-1.1547 EndZ=0
    g4: LineSegment StartX=2 StartY=-1.1547 StartZ=0 EndX=2 EndY=1.1547 EndZ=0
    g5: LineSegment StartX=2 StartY=1.1547 StartZ=0 EndX=0 EndY=2.3094 EndZ=0
    g6: Circle [constr] CenterX=0 CenterY=0 CenterZ=0 NormalX=0 NormalY=0 NormalZ=1 AngleXU=0 Radius=2.3094
    g7: Circle CenterX=0 CenterY=0 CenterZ=0 NormalX=0 NormalY=0 NormalZ=1 AngleXU=0 Radius=1
  constraints (18):
    c: Coincident(g0,g1)
    c: Coincident(g1,g2)
    c: Coincident(g2,g3)
    c: Coincident(g3,g4)
    c: Coincident(g4,g5)
    c: Coincident(g5,g0)
    c: Equal(g0, g1-g5) x5
    c: PointOnObject(g0,g6)
    c: PointOnObject(g1,g6)
    c: PointOnObject(g2,g6)
    c: PointOnObject(g3,g6)
    c: PointOnObject(g4,g6)
    c: PointOnObject(g5,g6)
    c: Coincident(g6,g-1)
    c: PointOnObject(g5,g-2)
    c: DistanceX(g0,g4) = 4
    c: Coincident(g7,g-1)
    c: Radius(g7) = 1
FEATURE [PartDesign::Pad] Pad858  label="M3 Nut Primitive169"
  Length = 0.6
  Length2 = 0.6
  Profile = -> Sketch1965
  Type = 4
FEATURE [Sketcher::SketchObject] Sketch1967
  ExternalGeometry = -> [Pad858]
  MapMode = 5
  Placement = pos=(0,0,0) rot=(0.57735,0.57735,0.57735;2.0944rad)
  Support = -> [YZ_Plane732]
  sketch-geometry (6):
    g0: LineSegment StartX=-1.9594 StartY=0.6 StartZ=0 EndX=-2.8094 EndY=0.6 EndZ=0
    g1: LineSegment StartX=-2.8094 StartY=0.6 StartZ=0 EndX=-2.8094 EndY=-0.6 EndZ=0
    g2: LineSegment StartX=-2.8094 StartY=-0.6 StartZ=0 EndX=-1.9594 EndY=-0.6 EndZ=0
    g3: LineSegment StartX=-1.9594 StartY=-0.6 StartZ=0 EndX=-2.3094 EndY=-0.4 EndZ=0
    g4: LineSegment StartX=-2.3094 StartY=-0.4 StartZ=0 EndX=-2.3094 EndY=0.4 EndZ=0
    g5: LineSegment StartX=-2.3094 StartY=0.4 StartZ=0 EndX=-1.9594 EndY=0.6 EndZ=0
  constraints (15):
    c: Horizontal(g0)
    c: Coincident(g0,g1)
    c: Coincident(g1,g2)
    c: Coincident(g2,g3)
    c: Coincident(g3,g4)
    c: Coincident(g4,g5)
    c: Coincident(g5,g0)
    c: Symmetric(g4,g3,g-1)
    c: Symmetric(g0,g2,g-1)
    c: Symmetric(g1,g0,g-1)
    c: DistanceX(g0,g4) = 0.5
    c: DistanceY(g3,g4) = 0.8
    c: DistanceY(g1,g0) = 1.2
    c: PointOnObject(g3,g-3)
    c: DistanceX(g4,g0) = 0.35
FEATURE [PartDesign::Groove] Groove180  label="M3 Nut Smooth172"
  Angle = 360
  Axis = (-2e-16,3e-16,1)
  Base = (0,0,0)
  BaseFeature = -> Pad858
  Profile = -> Sketch1967
  ReferenceAxis = -> Sketch1967 [V_Axis]
  Reversed = true
FEATURE [PartDesign::Chamfer] Chamfer400  label="M3 Nut Smooth Hole166"
  Base = -> Groove180 [Edge24,Edge23]
  BaseFeature = -> Groove180
  Size = 0.2
FEATURE [Sketcher::SketchObject] Sketch1968
  MapMode = 5
  Support = -> [XY_Plane762]
  sketch-geometry (1):
    g0: Circle CenterX=0 CenterY=0 CenterZ=0 NormalX=0 NormalY=0 NormalZ=1 AngleXU=0 Radius=1.9
  constraints (2):
    c: Coincident(g0,g-1)
    c: Radius(g0) = 1.9
FEATURE [PartDesign::Pad] Pad853  label="M3x8 Head109"
  Length = 2
  Length2 = 100
  Profile = -> Sketch1968
  Type = 0
FEATURE [Sketcher::SketchObject] Sketch1969
  MapMode = 5
  Support = -> [XY_Plane741]
  sketch-geometry (1):
    g0: Circle CenterX=0 CenterY=0 CenterZ=0 NormalX=0 NormalY=0 NormalZ=1 AngleXU=0 Radius=2.75
  constraints (2):
    c: Coincident(g0,g-1)
    c: Radius(g0) = 2.75
FEATURE [PartDesign::Pad] Pad851  label="M3x8 Head107"
  Length = 3
  Length2 = 100
  Profile = -> Sketch1969
  Type = 0
FEATURE [Sketcher::SketchObject] Sketch1970
  MapMode = 5
  Placement = pos=(0,0,2) rot=(0,0,1;0rad)
  Support = -> [Pad853]
  sketch-geometry (1):
    g0: Circle CenterX=0 CenterY=0 CenterZ=0 NormalX=0 NormalY=0 NormalZ=1 AngleXU=0 Radius=1
  constraints (2):
    c: Coincident(g0,g-1)
    c: Radius(g0) = 1
FEATURE [PartDesign::Pad] Pad849  label="M3x8 Thread106"
  BaseFeature = -> Pad853
  Length = 8
  Length2 = 100
  Profile = -> Sketch1970
  Type = 0
FEATURE [Sketcher::SketchObject] Sketch1962
  MapMode = 5
  Placement = pos=(0,0,0) rot=(1,0,0;3.14159rad)
  Support = -> [Pad849]
  sketch-geometry (7):
    g0: LineSegment StartX=0.77 StartY=0.44456 StartZ=0 EndX=0 EndY=0.889119 EndZ=0
    g1: LineSegment StartX=0 StartY=0.889119 StartZ=0 EndX=-0.77 EndY=0.44456 EndZ=0
    g2: LineSegment StartX=-0.77 StartY=0.44456 StartZ=0 EndX=-0.77 EndY=-0.44456 EndZ=0
    g3: LineSegment StartX=-0.77 StartY=-0.44456 StartZ=0 EndX=3.85628e-11 EndY=-0.889119 EndZ=0
    g4: LineSegment StartX=3.85628e-11 StartY=-0.889119 StartZ=0 EndX=0.77 EndY=-0.44456 EndZ=0
    g5: LineSegment StartX=0.77 StartY=-0.44456 StartZ=0 EndX=0.77 EndY=0.44456 EndZ=0
    g6: Circle [constr] CenterX=0 CenterY=0 CenterZ=0 NormalX=0 NormalY=0 NormalZ=1 AngleXU=0 Radius=0.889119
  constraints (16):
    c: Coincident(g0,g1)
    c: Coincident(g1,g2)
    c: Coincident(g2,g3)
    c: Coincident(g3,g4)
    c: Coincident(g4,g5)
    c: Coincident(g5,g0)
    c: Equal(g0, g1-g5) x5
    c: PointOnObject(g0,g6)
    c: PointOnObject(g1,g6)
    c: PointOnObject(g2,g6)
    c: PointOnObject(g3,g6)
    c: PointOnObject(g4,g6)
    c: PointOnObject(g5,g6)
    c: Coincident(g6,g-1)
    c: PointOnObject(g0,g-2)
    c: DistanceX(g1,g0) = 1.54
FEATURE [PartDesign::Pocket] Pocket715  label="M3x8 Wrench106"
  BaseFeature = -> Pad849
  Length = 1
  Length2 = 100
  Profile = -> Sketch1962
  Type = 0
FEATURE [PartDesign::Chamfer] Chamfer410  label="M3x8 Smooth111"
  Base = -> Pocket715 [Face11,Edge2,Edge24,Edge3]
  BaseFeature = -> Pocket715
  Size = 0.2
FEATURE [PartDesign::Body] Body535  label="M2x075"
  Group = -> [Sketch1968,Pad853,Sketch1970,Pad849,Sketch1962,Pocket715,Chamfer410]
  Origin = -> Origin758
  Tip = -> Chamfer410
FEATURE [Sketcher::SketchObject] Sketch1971
  MapMode = 5
  Support = -> [XY_Plane749]
  sketch-geometry (8):
    g0: LineSegment StartX=0 StartY=2.3094 StartZ=0 EndX=-2 EndY=1.1547 EndZ=0
    g1: LineSegment StartX=-2 StartY=1.1547 StartZ=0 EndX=-2 EndY=-1.1547 EndZ=0
    g2: LineSegment StartX=-2 StartY=-1.1547 StartZ=0 EndX=-2e-16 EndY=-2.3094 EndZ=0
    g3: LineSegment StartX=-2e-16 StartY=-2.3094 StartZ=0 EndX=2 EndY=-1.1547 EndZ=0
    g4: LineSegment StartX=2 StartY=-1.1547 StartZ=0 EndX=2 EndY=1.1547 EndZ=0
    g5: LineSegment StartX=2 StartY=1.1547 StartZ=0 EndX=0 EndY=2.3094 EndZ=0
    g6: Circle [constr] CenterX=0 CenterY=0 CenterZ=0 NormalX=0 NormalY=0 NormalZ=1 AngleXU=0 Radius=2.3094
    g7: Circle CenterX=0 CenterY=0 CenterZ=0 NormalX=0 NormalY=0 NormalZ=1 AngleXU=0 Radius=1
  constraints (18):
    c: Coincident(g0,g1)
    c: Coincident(g1,g2)
    c: Coincident(g2,g3)
    c: Coincident(g3,g4)
    c: Coincident(g4,g5)
    c: Coincident(g5,g0)
    c: Equal(g0, g1-g5) x5
    c: PointOnObject(g0,g6)
    c: PointOnObject(g1,g6)
    c: PointOnObject(g2,g6)
    c: PointOnObject(g3,g6)
    c: PointOnObject(g4,g6)
    c: PointOnObject(g5,g6)
    c: Coincident(g6,g-1)
    c: PointOnObject(g5,g-2)
    c: DistanceX(g0,g4) = 4
    c: Coincident(g7,g-1)
    c: Radius(g7) = 1
FEATURE [PartDesign::Pad] Pad863  label="M3 Nut Primitive171"
  Length = 0.6
  Length2 = 0.6
  Profile = -> Sketch1971
  Type = 4
FEATURE [Sketcher::SketchObject] Sketch1972
  MapMode = 5
  Support = -> [XY_Plane738]
FEATURE [PartDesign::Body] Body550  label="M2 Nut068"
  Group = -> [Sketch1965,Pad858,Sketch1967,Groove180,Chamfer400,Sketch1972,Sketch1957]
  Origin = -> Origin772
  Placement = pos=(0,0,2.75) rot=(0,0,1;0rad)
  Tip = -> Chamfer400
FEATURE [App::Part] Part215  label="M066"
  Group = -> [Body535,Body550]
  Origin = -> Origin775
  Placement = pos=(-9.1,5.25,80) rot=(0,1,0;3.14159rad)
FEATURE [Sketcher::SketchObject] Sketch1974
  MapMode = 5
  Support = -> [XY_Plane749]
FEATURE [Sketcher::SketchObject] Sketch1975
  MapMode = 5
  Support = -> [XY_Plane755]
  sketch-geometry (8):
    g0: LineSegment StartX=0 StartY=3.17543 StartZ=0 EndX=-2.75 EndY=1.58771 EndZ=0
    g1: LineSegment StartX=-2.75 StartY=1.58771 StartZ=0 EndX=-2.75 EndY=-1.58771 EndZ=0
    g2: LineSegment StartX=-2.75 StartY=-1.58771 StartZ=0 EndX=0 EndY=-3.17543 EndZ=0
    g3: LineSegment StartX=0 StartY=-3.17543 StartZ=0 EndX=2.75 EndY=-1.58771 EndZ=0
    g4: LineSegment StartX=2.75 StartY=-1.58771 StartZ=0 EndX=2.75 EndY=1.58771 EndZ=0
    g5: LineSegment StartX=2.75 StartY=1.58771 StartZ=0 EndX=0 EndY=3.17543 EndZ=0
    g6: Circle [constr] CenterX=0 CenterY=0 CenterZ=0 NormalX=0 NormalY=0 NormalZ=1 AngleXU=0 Radius=3.17543
    g7: Circle CenterX=0 CenterY=0 CenterZ=0 NormalX=0 NormalY=0 NormalZ=1 AngleXU=0 Radius=1.5
  constraints (18):
    c: Coincident(g0,g1)
    c: Coincident(g1,g2)
    c: Coincident(g2,g3)
    c: Coincident(g3,g4)
    c: Coincident(g4,g5)
    c: Coincident(g5,g0)
    c: Equal(g0, g1-g5) x5
    c: PointOnObject(g0,g6)
    c: PointOnObject(g1,g6)
    c: PointOnObject(g2,g6)
    c: PointOnObject(g3,g6)
    c: PointOnObject(g4,g6)
    c: PointOnObject(g5,g6)
    c: Coincident(g6,g-1)
    c: PointOnObject(g5,g-2)
    c: DistanceX(g0,g4) = 5.5
    c: Coincident(g7,g-1)
    c: Radius(g7) = 1.5
FEATURE [PartDesign::Pad] Pad860  label="M3 Nut Primitive170"
  Length = 1.2
  Length2 = 1.2
  Profile = -> Sketch1975
  Type = 4
FEATURE [Sketcher::SketchObject] Sketch1976
  MapMode = 5
  Support = -> [XY_Plane756]
  sketch-geometry (8):
    g0: LineSegment StartX=0 StartY=3.17543 StartZ=0 EndX=-2.75 EndY=1.58771 EndZ=0
    g1: LineSegment StartX=-2.75 StartY=1.58771 StartZ=0 EndX=-2.75 EndY=-1.58771 EndZ=0
    g2: LineSegment StartX=-2.75 StartY=-1.58771 StartZ=0 EndX=0 EndY=-3.17543 EndZ=0
    g3: LineSegment StartX=0 StartY=-3.17543 StartZ=0 EndX=2.75 EndY=-1.58771 EndZ=0
    g4: LineSegment StartX=2.75 StartY=-1.58771 StartZ=0 EndX=2.75 EndY=1.58771 EndZ=0
    g5: LineSegment StartX=2.75 StartY=1.58771 StartZ=0 EndX=0 EndY=3.17543 EndZ=0
    g6: Circle [constr] CenterX=0 CenterY=0 CenterZ=0 NormalX=0 NormalY=0 NormalZ=1 AngleXU=0 Radius=3.17543
    g7: Circle CenterX=0 CenterY=0 CenterZ=0 NormalX=0 NormalY=0 NormalZ=1 AngleXU=0 Radius=1.5
  constraints (18):
    c: Coincident(g0,g1)
    c: Coincident(g1,g2)
    c: Coincident(g2,g3)
    c: Coincident(g3,g4)
    c: Coincident(g4,g5)
    c: Coincident(g5,g0)
    c: Equal(g0, g1-g5) x5
    c: PointOnObject(g0,g6)
    c: PointOnObject(g1,g6)
    c: PointOnObject(g2,g6)
    c: PointOnObject(g3,g6)
    c: PointOnObject(g4,g6)
    c: PointOnObject(g5,g6)
    c: Coincident(g6,g-1)
    c: PointOnObject(g5,g-2)
    c: DistanceX(g0,g4) = 5.5
    c: Coincident(g7,g-1)
    c: Radius(g7) = 1.5
FEATURE [PartDesign::Pad] Pad869  label="M3 Nut Primitive174"
  Length = 1.2
  Length2 = 1.2
  Profile = -> Sketch1976
  Type = 4
FEATURE [Sketcher::SketchObject] Sketch1977
  MapMode = 5
  Support = -> [XY_Plane757]
  sketch-geometry (1):
    g0: Circle CenterX=0 CenterY=0 CenterZ=0 NormalX=0 NormalY=0 NormalZ=1 AngleXU=0 Radius=2.75
  constraints (2):
    c: Coincident(g0,g-1)
    c: Radius(g0) = 2.75
FEATURE [PartDesign::Pad] Pad834  label="M3x8 Head101"
  Length = 3
  Length2 = 100
  Profile = -> Sketch1977
  Type = 0
FEATURE [Sketcher::SketchObject] Sketch1978
  MapMode = 5
  Support = -> [XY_Plane749]
FEATURE [Sketcher::SketchObject] Sketch1979
  ExternalGeometry = -> [Pad863]
  MapMode = 5
  Placement = pos=(0,0,0) rot=(0.57735,0.57735,0.57735;2.0944rad)
  Support = -> [YZ_Plane738]
  sketch-geometry (6):
    g0: LineSegment StartX=-1.9594 StartY=0.6 StartZ=0 EndX=-2.8094 EndY=0.6 EndZ=0
    g1: LineSegment StartX=-2.8094 StartY=0.6 StartZ=0 EndX=-2.8094 EndY=-0.6 EndZ=0
    g2: LineSegment StartX=-2.8094 StartY=-0.6 StartZ=0 EndX=-1.9594 EndY=-0.6 EndZ=0
    g3: LineSegment StartX=-1.9594 StartY=-0.6 StartZ=0 EndX=-2.3094 EndY=-0.4 EndZ=0
    g4: LineSegment StartX=-2.3094 StartY=-0.4 StartZ=0 EndX=-2.3094 EndY=0.4 EndZ=0
    g5: LineSegment StartX=-2.3094 StartY=0.4 StartZ=0 EndX=-1.9594 EndY=0.6 EndZ=0
  constraints (15):
    c: Horizontal(g0)
    c: Coincident(g0,g1)
    c: Coincident(g1,g2)
    c: Coincident(g2,g3)
    c: Coincident(g3,g4)
    c: Coincident(g4,g5)
    c: Coincident(g5,g0)
    c: Symmetric(g4,g3,g-1)
    c: Symmetric(g0,g2,g-1)
    c: Symmetric(g1,g0,g-1)
    c: DistanceX(g0,g4) = 0.5
    c: DistanceY(g3,g4) = 0.8
    c: DistanceY(g1,g0) = 1.2
    c: PointOnObject(g3,g-3)
    c: DistanceX(g4,g0) = 0.35
FEATURE [PartDesign::Groove] Groove179  label="M3 Nut Smooth171"
  Angle = 360
  Axis = (-2e-16,3e-16,1)
  Base = (0,0,0)
  BaseFeature = -> Pad863
  Profile = -> Sketch1979
  ReferenceAxis = -> Sketch1979 [V_Axis]
  Reversed = true
FEATURE [PartDesign::Chamfer] Chamfer402  label="M3 Nut Smooth Hole168"
  Base = -> Groove179 [Edge24,Edge23]
  BaseFeature = -> Groove179
  Size = 0.2
FEATURE [PartDesign::Body] Body540  label="M2 Nut064"
  Group = -> [Sketch1971,Pad863,Sketch1979,Groove179,Chamfer402,Sketch1974,Sketch1978]
  Origin = -> Origin773
  Placement = pos=(-19.5,10,15) rot=(0.57735,0.57735,-0.57735;4.18879rad)
  Tip = -> Chamfer402
FEATURE [Sketcher::SketchObject] Sketch1980
  ExternalGeometry = -> [Pad860]
  MapMode = 5
  Placement = pos=(0,0,0) rot=(0.57735,0.57735,0.57735;2.0944rad)
  Support = -> [YZ_Plane741]
  sketch-geometry (6):
    g0: LineSegment StartX=-2.67543 StartY=1.2 StartZ=0 EndX=-3.67543 EndY=1.2 EndZ=0
    g1: LineSegment StartX=-3.67543 StartY=1.2 StartZ=0 EndX=-3.67543 EndY=-1.2 EndZ=0
    g2: LineSegment StartX=-3.67543 StartY=-1.2 StartZ=0 EndX=-2.67543 EndY=-1.2 EndZ=0
    g3: LineSegment StartX=-2.67543 StartY=-1.2 StartZ=0 EndX=-3.17543 EndY=-1 EndZ=0
    g4: LineSegment StartX=-3.17543 StartY=-1 StartZ=0 EndX=-3.17543 EndY=1 EndZ=0
    g5: LineSegment StartX=-3.17543 StartY=1 StartZ=0 EndX=-2.67543 EndY=1.2 EndZ=0
  constraints (15):
    c: Horizontal(g0)
    c: Coincident(g0,g1)
    c: Coincident(g1,g2)
    c: Coincident(g2,g3)
    c: Coincident(g3,g4)
    c: Coincident(g4,g5)
    c: Coincident(g5,g0)
    c: Symmetric(g4,g3,g-1)
    c: Symmetric(g0,g2,g-1)
    c: Symmetric(g1,g0,g-1)
    c: DistanceX(g0,g4) = 0.5
    c: DistanceY(g3,g4) = 2
    c: DistanceY(g1,g0) = 2.4
    c: PointOnObject(g3,g-3)
    c: DistanceX(g4,g0) = 0.5
FEATURE [PartDesign::Groove] Groove176  label="M3 Nut Smooth168"
  Angle = 360
  Axis = (-2e-16,3e-16,1)
  Base = (0,0,0)
  BaseFeature = -> Pad860
  Profile = -> Sketch1980
  ReferenceAxis = -> Sketch1980 [V_Axis]
  Reversed = true
FEATURE [PartDesign::Chamfer] Chamfer411  label="M3 Nut Smooth Hole172"
  Base = -> Groove176 [Edge24,Edge23]
  BaseFeature = -> Groove176
  Size = 0.2
FEATURE [PartDesign::Body] Body531  label="M3 Nut097"
  Group = -> [Sketch1975,Pad860,Sketch1980,Groove176,Chamfer411]
  Origin = -> Origin768
  Placement = pos=(-14.15,14.15,3.5) rot=(0,0,1;0.261799rad)
  Tip = -> Chamfer411
FEATURE [Sketcher::SketchObject] Sketch1981
  ExternalGeometry = -> [Pad869]
  MapMode = 5
  Placement = pos=(0,0,0) rot=(0.57735,0.57735,0.57735;2.0944rad)
  Support = -> [YZ_Plane744]
  sketch-geometry (6):
    g0: LineSegment StartX=-2.67543 StartY=1.2 StartZ=0 EndX=-3.67543 EndY=1.2 EndZ=0
    g1: LineSegment StartX=-3.67543 StartY=1.2 StartZ=0 EndX=-3.67543 EndY=-1.2 EndZ=0
    g2: LineSegment StartX=-3.67543 StartY=-1.2 StartZ=0 EndX=-2.67543 EndY=-1.2 EndZ=0
    g3: LineSegment StartX=-2.67543 StartY=-1.2 StartZ=0 EndX=-3.17543 EndY=-1 EndZ=0
    g4: LineSegment StartX=-3.17543 StartY=-1 StartZ=0 EndX=-3.17543 EndY=1 EndZ=0
    g5: LineSegment StartX=-3.17543 StartY=1 StartZ=0 EndX=-2.67543 EndY=1.2 EndZ=0
  constraints (15):
    c: Horizontal(g0)
    c: Coincident(g0,g1)
    c: Coincident(g1,g2)
    c: Coincident(g2,g3)
    c: Coincident(g3,g4)
    c: Coincident(g4,g5)
    c: Coincident(g5,g0)
    c: Symmetric(g4,g3,g-1)
    c: Symmetric(g0,g2,g-1)
    c: Symmetric(g1,g0,g-1)
    c: DistanceX(g0,g4) = 0.5
    c: DistanceY(g3,g4) = 2
    c: DistanceY(g1,g0) = 2.4
    c: PointOnObject(g3,g-3)
    c: DistanceX(g4,g0) = 0.5
FEATURE [PartDesign::Groove] Groove174  label="M3 Nut Smooth166"
  Angle = 360
  Axis = (-2e-16,3e-16,1)
  Base = (0,0,0)
  BaseFeature = -> Pad869
  Profile = -> Sketch1981
  ReferenceAxis = -> Sketch1981 [V_Axis]
  Reversed = true
FEATURE [PartDesign::Chamfer] Chamfer412  label="M3 Nut Smooth Hole173"
  Base = -> Groove174 [Edge24,Edge23]
  BaseFeature = -> Groove174
  Size = 0.2
FEATURE [PartDesign::Body] Body528  label="M3 Nut095"
  Group = -> [Sketch1976,Pad869,Sketch1981,Groove174,Chamfer412]
  Origin = -> Origin776
  Placement = pos=(-14.15,-14.15,3.5) rot=(0,0,-1;0.261799rad)
  Tip = -> Chamfer412
FEATURE [Sketcher::SketchObject] Sketch1983
  MapMode = 5
  Support = -> [XY_Plane750]
  sketch-geometry (1):
    g0: Circle CenterX=0 CenterY=0 CenterZ=0 NormalX=0 NormalY=0 NormalZ=1 AngleXU=0 Radius=1.9
  constraints (2):
    c: Coincident(g0,g-1)
    c: Radius(g0) = 1.9
FEATURE [PartDesign::Pad] Pad837  label="M3x8 Head104"
  Length = 2
  Length2 = 100
  Profile = -> Sketch1983
  Type = 0
FEATURE [Sketcher::SketchObject] Sketch1966
  MapMode = 5
  Placement = pos=(0,0,2) rot=(0,0,1;0rad)
  Support = -> [Pad837]
  sketch-geometry (1):
    g0: Circle CenterX=0 CenterY=0 CenterZ=0 NormalX=0 NormalY=0 NormalZ=1 AngleXU=0 Radius=1
  constraints (2):
    c: Coincident(g0,g-1)
    c: Radius(g0) = 1
FEATURE [PartDesign::Pad] Pad833  label="M3x8 Thread103"
  BaseFeature = -> Pad837
  Length = 8
  Length2 = 100
  Profile = -> Sketch1966
  Type = 0
FEATURE [Sketcher::SketchObject] Sketch1954
  MapMode = 5
  Placement = pos=(0,0,0) rot=(1,0,0;3.14159rad)
  Support = -> [Pad833]
  sketch-geometry (7):
    g0: LineSegment StartX=0.77 StartY=0.44456 StartZ=0 EndX=0 EndY=0.889119 EndZ=0
    g1: LineSegment StartX=0 StartY=0.889119 StartZ=0 EndX=-0.77 EndY=0.44456 EndZ=0
    g2: LineSegment StartX=-0.77 StartY=0.44456 StartZ=0 EndX=-0.77 EndY=-0.44456 EndZ=0
    g3: LineSegment StartX=-0.77 StartY=-0.44456 StartZ=0 EndX=3.85628e-11 EndY=-0.889119 EndZ=0
    g4: LineSegment StartX=3.85628e-11 StartY=-0.889119 StartZ=0 EndX=0.77 EndY=-0.44456 EndZ=0
    g5: LineSegment StartX=0.77 StartY=-0.44456 StartZ=0 EndX=0.77 EndY=0.44456 EndZ=0
    g6: Circle [constr] CenterX=0 CenterY=0 CenterZ=0 NormalX=0 NormalY=0 NormalZ=1 AngleXU=0 Radius=0.889119
  constraints (16):
    c: Coincident(g0,g1)
    c: Coincident(g1,g2)
    c: Coincident(g2,g3)
    c: Coincident(g3,g4)
    c: Coincident(g4,g5)
    c: Coincident(g5,g0)
    c: Equal(g0, g1-g5) x5
    c: PointOnObject(g0,g6)
    c: PointOnObject(g1,g6)
    c: PointOnObject(g2,g6)
    c: PointOnObject(g3,g6)
    c: PointOnObject(g4,g6)
    c: PointOnObject(g5,g6)
    c: Coincident(g6,g-1)
    c: PointOnObject(g0,g-2)
    c: DistanceX(g1,g0) = 1.54
FEATURE [PartDesign::Pocket] Pocket709  label="M3x8 Wrench101"
  BaseFeature = -> Pad833
  Length = 1
  Length2 = 100
  Profile = -> Sketch1954
  Type = 0
FEATURE [PartDesign::Chamfer] Chamfer396  label="M3x8 Smooth103"
  Base = -> Pocket709 [Face11,Edge2,Edge24,Edge3]
  BaseFeature = -> Pocket709
  Size = 0.2
FEATURE [PartDesign::Body] Body553  label="M2x079"
  Group = -> [Sketch1983,Pad837,Sketch1966,Pad833,Sketch1954,Pocket709,Chamfer396]
  Origin = -> Origin740
  Placement = pos=(-28.75,10,15) rot=(0,1,0;1.5708rad)
  Tip = -> Chamfer396
FEATURE [App::Part] Part210  label="SHOULDER PIN003"
  Group = -> [Body540,Body553,Body545]
  Origin = -> Origin760
FEATURE [Sketcher::SketchObject] Sketch1984
  MapMode = 5
  Support = -> [XY_Plane740]
  sketch-geometry (1):
    g0: Circle CenterX=0 CenterY=0 CenterZ=0 NormalX=0 NormalY=0 NormalZ=1 AngleXU=0 Radius=2.75
  constraints (2):
    c: Coincident(g0,g-1)
    c: Radius(g0) = 2.75
FEATURE [PartDesign::Pad] Pad855  label="M3x8 Head110"
  Length = 3
  Length2 = 100
  Profile = -> Sketch1984
  Type = 0
FEATURE [Sketcher::SketchObject] Sketch1986
  MapMode = 5
  Support = -> [XY_Plane753]
  sketch-geometry (8):
    g0: LineSegment StartX=0 StartY=3.17543 StartZ=0 EndX=-2.75 EndY=1.58771 EndZ=0
    g1: LineSegment StartX=-2.75 StartY=1.58771 StartZ=0 EndX=-2.75 EndY=-1.58771 EndZ=0
    g2: LineSegment StartX=-2.75 StartY=-1.58771 StartZ=0 EndX=0 EndY=-3.17543 EndZ=0
    g3: LineSegment StartX=0 StartY=-3.17543 StartZ=0 EndX=2.75 EndY=-1.58771 EndZ=0
    g4: LineSegment StartX=2.75 StartY=-1.58771 StartZ=0 EndX=2.75 EndY=1.58771 EndZ=0
    g5: LineSegment StartX=2.75 StartY=1.58771 StartZ=0 EndX=0 EndY=3.17543 EndZ=0
    g6: Circle [constr] CenterX=0 CenterY=0 CenterZ=0 NormalX=0 NormalY=0 NormalZ=1 AngleXU=0 Radius=3.17543
    g7: Circle CenterX=0 CenterY=0 CenterZ=0 NormalX=0 NormalY=0 NormalZ=1 AngleXU=0 Radius=1.5
  constraints (18):
    c: Coincident(g0,g1)
    c: Coincident(g1,g2)
    c: Coincident(g2,g3)
    c: Coincident(g3,g4)
    c: Coincident(g4,g5)
    c: Coincident(g5,g0)
    c: Equal(g0, g1-g5) x5
    c: PointOnObject(g0,g6)
    c: PointOnObject(g1,g6)
    c: PointOnObject(g2,g6)
    c: PointOnObject(g3,g6)
    c: PointOnObject(g4,g6)
    c: PointOnObject(g5,g6)
    c: Coincident(g6,g-1)
    c: PointOnObject(g5,g-2)
    c: DistanceX(g0,g4) = 5.5
    c: Coincident(g7,g-1)
    c: Radius(g7) = 1.5
FEATURE [PartDesign::Pad] Pad864  label="M3 Nut Primitive172"
  Length = 1.2
  Length2 = 1.2
  Profile = -> Sketch1986
  Type = 4
FEATURE [Sketcher::SketchObject] Sketch1985
  ExternalGeometry = -> [Pad864]
  MapMode = 5
  Placement = pos=(0,0,0) rot=(0.57735,0.57735,0.57735;2.0944rad)
  Support = -> [YZ_Plane734]
  sketch-geometry (6):
    g0: LineSegment StartX=-2.67543 StartY=1.2 StartZ=0 EndX=-3.67543 EndY=1.2 EndZ=0
    g1: LineSegment StartX=-3.67543 StartY=1.2 StartZ=0 EndX=-3.67543 EndY=-1.2 EndZ=0
    g2: LineSegment StartX=-3.67543 StartY=-1.2 StartZ=0 EndX=-2.67543 EndY=-1.2 EndZ=0
    g3: LineSegment StartX=-2.67543 StartY=-1.2 StartZ=0 EndX=-3.17543 EndY=-1 EndZ=0
    g4: LineSegment StartX=-3.17543 StartY=-1 StartZ=0 EndX=-3.17543 EndY=1 EndZ=0
    g5: LineSegment StartX=-3.17543 StartY=1 StartZ=0 EndX=-2.67543 EndY=1.2 EndZ=0
  constraints (15):
    c: Horizontal(g0)
    c: Coincident(g0,g1)
    c: Coincident(g1,g2)
    c: Coincident(g2,g3)
    c: Coincident(g3,g4)
    c: Coincident(g4,g5)
    c: Coincident(g5,g0)
    c: Symmetric(g4,g3,g-1)
    c: Symmetric(g0,g2,g-1)
    c: Symmetric(g1,g0,g-1)
    c: DistanceX(g0,g4) = 0.5
    c: DistanceY(g3,g4) = 2
    c: DistanceY(g1,g0) = 2.4
    c: PointOnObject(g3,g-3)
    c: DistanceX(g4,g0) = 0.5
FEATURE [PartDesign::Groove] Groove182  label="M3 Nut Smooth174"
  Angle = 360
  Axis = (-2e-16,3e-16,1)
  Base = (0,0,0)
  BaseFeature = -> Pad864
  Profile = -> Sketch1985
  ReferenceAxis = -> Sketch1985 [V_Axis]
  Reversed = true
FEATURE [PartDesign::Chamfer] Chamfer404  label="M3 Nut Smooth Hole169"
  Base = -> Groove182 [Edge24,Edge23]
  BaseFeature = -> Groove182
  Size = 0.2
FEATURE [PartDesign::Body] Body538  label="M3 Nut098"
  Group = -> [Sketch1986,Pad864,Sketch1985,Groove182,Chamfer404]
  Origin = -> Origin761
  Placement = pos=(14.15,14.15,3.5) rot=(0,0,-1;0.261799rad)
  Tip = -> Chamfer404
FEATURE [Sketcher::SketchObject] Sketch1988
  MapMode = 5
  Support = -> [XY_Plane743]
  sketch-geometry (8):
    g0: LineSegment StartX=0 StartY=3.17543 StartZ=0 EndX=-2.75 EndY=1.58771 EndZ=0
    g1: LineSegment StartX=-2.75 StartY=1.58771 StartZ=0 EndX=-2.75 EndY=-1.58771 EndZ=0
    g2: LineSegment StartX=-2.75 StartY=-1.58771 StartZ=0 EndX=0 EndY=-3.17543 EndZ=0
    g3: LineSegment StartX=0 StartY=-3.17543 StartZ=0 EndX=2.75 EndY=-1.58771 EndZ=0
    g4: LineSegment StartX=2.75 StartY=-1.58771 StartZ=0 EndX=2.75 EndY=1.58771 EndZ=0
    g5: LineSegment StartX=2.75 StartY=1.58771 StartZ=0 EndX=0 EndY=3.17543 EndZ=0
    g6: Circle [constr] CenterX=0 CenterY=0 CenterZ=0 NormalX=0 NormalY=0 NormalZ=1 AngleXU=0 Radius=3.17543
    g7: Circle CenterX=0 CenterY=0 CenterZ=0 NormalX=0 NormalY=0 NormalZ=1 AngleXU=0 Radius=1.5
  constraints (18):
    c: Coincident(g0,g1)
    c: Coincident(g1,g2)
    c: Coincident(g2,g3)
    c: Coincident(g3,g4)
    c: Coincident(g4,g5)
    c: Coincident(g5,g0)
    c: Equal(g0, g1-g5) x5
    c: PointOnObject(g0,g6)
    c: PointOnObject(g1,g6)
    c: PointOnObject(g2,g6)
    c: PointOnObject(g3,g6)
    c: PointOnObject(g4,g6)
    c: PointOnObject(g5,g6)
    c: Coincident(g6,g-1)
    c: PointOnObject(g5,g-2)
    c: DistanceX(g0,g4) = 5.5
    c: Coincident(g7,g-1)
    c: Radius(g7) = 1.5
FEATURE [PartDesign::Pad] Pad868  label="M3 Nut Primitive173"
  Length = 1.2
  Length2 = 1.2
  Profile = -> Sketch1988
  Type = 4
FEATURE [Sketcher::SketchObject] Sketch1987
  ExternalGeometry = -> [Pad868]
  MapMode = 5
  Placement = pos=(0,0,0) rot=(0.57735,0.57735,0.57735;2.0944rad)
  Support = -> [YZ_Plane746]
  sketch-geometry (6):
    g0: LineSegment StartX=-2.67543 StartY=1.2 StartZ=0 EndX=-3.67543 EndY=1.2 EndZ=0
    g1: LineSegment StartX=-3.67543 StartY=1.2 StartZ=0 EndX=-3.67543 EndY=-1.2 EndZ=0
    g2: LineSegment StartX=-3.67543 StartY=-1.2 StartZ=0 EndX=-2.67543 EndY=-1.2 EndZ=0
    g3: LineSegment StartX=-2.67543 StartY=-1.2 StartZ=0 EndX=-3.17543 EndY=-1 EndZ=0
    g4: LineSegment StartX=-3.17543 StartY=-1 StartZ=0 EndX=-3.17543 EndY=1 EndZ=0
    g5: LineSegment StartX=-3.17543 StartY=1 StartZ=0 EndX=-2.67543 EndY=1.2 EndZ=0
  constraints (15):
    c: Horizontal(g0)
    c: Coincident(g0,g1)
    c: Coincident(g1,g2)
    c: Coincident(g2,g3)
    c: Coincident(g3,g4)
    c: Coincident(g4,g5)
    c: Coincident(g5,g0)
    c: Symmetric(g4,g3,g-1)
    c: Symmetric(g0,g2,g-1)
    c: Symmetric(g1,g0,g-1)
    c: DistanceX(g0,g4) = 0.5
    c: DistanceY(g3,g4) = 2
    c: DistanceY(g1,g0) = 2.4
    c: PointOnObject(g3,g-3)
    c: DistanceX(g4,g0) = 0.5
FEATURE [PartDesign::Groove] Groove181  label="M3 Nut Smooth173"
  Angle = 360
  Axis = (-2e-16,3e-16,1)
  Base = (0,0,0)
  BaseFeature = -> Pad868
  Profile = -> Sketch1987
  ReferenceAxis = -> Sketch1987 [V_Axis]
  Reversed = true
FEATURE [PartDesign::Chamfer] Chamfer389  label="M3 Nut Smooth Hole164"
  Base = -> Groove181 [Edge24,Edge23]
  BaseFeature = -> Groove181
  Size = 0.2
FEATURE [PartDesign::Body] Body530  label="M3 Nut096"
  Group = -> [Sketch1988,Pad868,Sketch1987,Groove181,Chamfer389]
  Origin = -> Origin743
  Placement = pos=(14.15,-14.15,3.5) rot=(0,0,1;0.261799rad)
  Tip = -> Chamfer389
FEATURE [App::Part] Part218  label="Shouldercap Nuts003"
  Group = -> [Body538,Body531,Body530,Body528]
  Origin = -> Origin747
FEATURE [Sketcher::SketchObject] Sketch1990
  MapMode = 5
  Placement = pos=(0,0,3) rot=(0,0,1;0rad)
  Support = -> [Pad851]
  sketch-geometry (1):
    g0: Circle CenterX=0 CenterY=0 CenterZ=0 NormalX=0 NormalY=0 NormalZ=1 AngleXU=0 Radius=1.5
  constraints (2):
    c: Coincident(g0,g-1)
    c: Radius(g0) = 1.5
FEATURE [PartDesign::Pad] Pad850  label="M3x8 Thread107"
  BaseFeature = -> Pad851
  Length = 8
  Length2 = 100
  Profile = -> Sketch1990
  Type = 0
FEATURE [Sketcher::SketchObject] Sketch1973
  MapMode = 5
  Placement = pos=(0,0,0) rot=(1,0,0;3.14159rad)
  Support = -> [Pad850]
  sketch-geometry (7):
    g0: LineSegment StartX=1.275 StartY=0.736122 StartZ=0 EndX=0 EndY=1.47224 EndZ=0
    g1: LineSegment StartX=0 StartY=1.47224 StartZ=0 EndX=-1.275 EndY=0.736122 EndZ=0
    g2: LineSegment StartX=-1.275 StartY=0.736122 StartZ=0 EndX=-1.275 EndY=-0.736122 EndZ=0
    g3: LineSegment StartX=-1.275 StartY=-0.736122 StartZ=0 EndX=1.34766e-11 EndY=-1.47224 EndZ=0
    g4: LineSegment StartX=1.34766e-11 StartY=-1.47224 StartZ=0 EndX=1.275 EndY=-0.736122 EndZ=0
    g5: LineSegment StartX=1.275 StartY=-0.736122 StartZ=0 EndX=1.275 EndY=0.736122 EndZ=0
    g6: Circle [constr] CenterX=0 CenterY=0 CenterZ=0 NormalX=0 NormalY=0 NormalZ=1 AngleXU=0 Radius=1.47224
  constraints (16):
    c: Coincident(g0,g1)
    c: Coincident(g1,g2)
    c: Coincident(g2,g3)
    c: Coincident(g3,g4)
    c: Coincident(g4,g5)
    c: Coincident(g5,g0)
    c: Equal(g0, g1-g5) x5
    c: PointOnObject(g0,g6)
    c: PointOnObject(g1,g6)
    c: PointOnObject(g2,g6)
    c: PointOnObject(g3,g6)
    c: PointOnObject(g4,g6)
    c: PointOnObject(g5,g6)
    c: Coincident(g6,g-1)
    c: PointOnObject(g0,g-2)
    c: DistanceX(g1,g0) = 2.55
FEATURE [PartDesign::Pocket] Pocket717  label="M3x8 Wrench108"
  BaseFeature = -> Pad850
  Length = 1.3
  Length2 = 100
  Profile = -> Sketch1973
  Type = 0
FEATURE [PartDesign::Chamfer] Chamfer406  label="M3x8 Smooth108"
  Base = -> Pocket717 [Face11,Edge2,Edge24,Edge3]
  BaseFeature = -> Pocket717
  Size = 0.2
FEATURE [PartDesign::Body] Body529  label="M3x112"
  Group = -> [Sketch1969,Pad851,Sketch1990,Pad850,Sketch1973,Pocket717,Chamfer406]
  Origin = -> Origin769
  Placement = pos=(14.15,14.15,-6) rot=(0,0,1;0rad)
  Tip = -> Chamfer406
FEATURE [Sketcher::SketchObject] Sketch1993
  MapMode = 5
  Support = -> [XY_Plane746]
  sketch-geometry (1):
    g0: Circle CenterX=0 CenterY=0 CenterZ=0 NormalX=0 NormalY=0 NormalZ=1 AngleXU=0 Radius=2.75
  constraints (2):
    c: Coincident(g0,g-1)
    c: Radius(g0) = 2.75
FEATURE [PartDesign::Pad] Pad859  label="M3x8 Head111"
  Length = 3
  Length2 = 100
  Profile = -> Sketch1993
  Type = 0
FEATURE [Sketcher::SketchObject] Sketch1991
  MapMode = 5
  Placement = pos=(0,0,3) rot=(0,0,1;0rad)
  Support = -> [Pad859]
  sketch-geometry (1):
    g0: Circle CenterX=0 CenterY=0 CenterZ=0 NormalX=0 NormalY=0 NormalZ=1 AngleXU=0 Radius=1.5
  constraints (2):
    c: Coincident(g0,g-1)
    c: Radius(g0) = 1.5
FEATURE [PartDesign::Pad] Pad862  label="M3x8 Thread110"
  BaseFeature = -> Pad859
  Length = 8
  Length2 = 100
  Profile = -> Sketch1991
  Type = 0
FEATURE [Sketcher::SketchObject] Sketch1989
  MapMode = 5
  Placement = pos=(0,0,0) rot=(1,0,0;3.14159rad)
  Support = -> [Pad862]
  sketch-geometry (7):
    g0: LineSegment StartX=1.275 StartY=0.736122 StartZ=0 EndX=0 EndY=1.47224 EndZ=0
    g1: LineSegment StartX=0 StartY=1.47224 StartZ=0 EndX=-1.275 EndY=0.736122 EndZ=0
    g2: LineSegment StartX=-1.275 StartY=0.736122 StartZ=0 EndX=-1.275 EndY=-0.736122 EndZ=0
    g3: LineSegment StartX=-1.275 StartY=-0.736122 StartZ=0 EndX=1.34766e-11 EndY=-1.47224 EndZ=0
    g4: LineSegment StartX=1.34766e-11 StartY=-1.47224 StartZ=0 EndX=1.275 EndY=-0.736122 EndZ=0
    g5: LineSegment StartX=1.275 StartY=-0.736122 StartZ=0 EndX=1.275 EndY=0.736122 EndZ=0
    g6: Circle [constr] CenterX=0 CenterY=0 CenterZ=0 NormalX=0 NormalY=0 NormalZ=1 AngleXU=0 Radius=1.47224
  constraints (16):
    c: Coincident(g0,g1)
    c: Coincident(g1,g2)
    c: Coincident(g2,g3)
    c: Coincident(g3,g4)
    c: Coincident(g4,g5)
    c: Coincident(g5,g0)
    c: Equal(g0, g1-g5) x5
    c: PointOnObject(g0,g6)
    c: PointOnObject(g1,g6)
    c: PointOnObject(g2,g6)
    c: PointOnObject(g3,g6)
    c: PointOnObject(g4,g6)
    c: PointOnObject(g5,g6)
    c: Coincident(g6,g-1)
    c: PointOnObject(g0,g-2)
    c: DistanceX(g1,g0) = 2.55
FEATURE [PartDesign::Pocket] Pocket731  label="M3x8 Wrench111"
  BaseFeature = -> Pad862
  Length = 1.3
  Length2 = 100
  Profile = -> Sketch1989
  Type = 0
FEATURE [PartDesign::Chamfer] Chamfer408  label="M3x8 Smooth109"
  Base = -> Pocket731 [Face11,Edge2,Edge24,Edge3]
  BaseFeature = -> Pocket731
  Size = 0.2
FEATURE [PartDesign::Body] Body532  label="M3x113"
  Group = -> [Sketch1993,Pad859,Sketch1991,Pad862,Sketch1989,Pocket731,Chamfer408]
  Origin = -> Origin774
  Placement = pos=(-14.15,-14.15,-6) rot=(0,0,1;0rad)
  Tip = -> Chamfer408
FEATURE [Sketcher::SketchObject] Sketch1995
  ExternalGeometry = -> [Fillet242]
  MapMode = 5
  Support = -> [XY_Plane737]
  sketch-geometry (3):
    g0: ArcOfCircle [constr] CenterX=-2e-16 CenterY=-3e-16 CenterZ=0 NormalX=0 NormalY=0 NormalZ=1 AngleXU=0 Radius=13.5 StartAngle=3.66519 EndAngle=5.75959
    g1: ArcOfCircle [constr] CenterX=-2e-16 CenterY=-3e-16 CenterZ=0 NormalX=0 NormalY=0 NormalZ=1 AngleXU=0 Radius=13.5 StartAngle=2.61799 EndAngle=3.66519
    g2: LineSegment StartX=-11.6913 StartY=-6.75 StartZ=0 EndX=11.6913 EndY=6.75 EndZ=0
  constraints (9):
    c: Coincident(g0,g-5)
    c: Coincident(g0,g-4)
    c: Coincident(g1,g0)
    c: Coincident(g1,g0)
    c: Angle(g0) = 2.0944
    c: Angle(g1) = 1.0472
    c: Coincident(g1,g-3)
    c: Coincident(g2,g0)
    c: Coincident(g2,g-6)
FEATURE [PartDesign::Body] Body551  label="Futuba FSH6B009"
  Group = -> [Sketch1931,Pad844,Sketch1913,Pocket711,Sketch1924,Pocket708,Sketch1912,Pocket706,Sketch1938,Pad843,Fillet242,Sketch1995]
  Origin = -> Origin755
  Tip = -> Fillet242
FEATURE [App::Part] Part208  label="Servphorn003"
  Group = -> [Body551]
  Origin = -> Origin753
  Placement = pos=(0,0,3.45) rot=(0,0,1;0rad)
FEATURE [Sketcher::SketchObject] Sketch1996
  MapMode = 5
  Placement = pos=(0,0,0) rot=(0.57735,0.57735,0.57735;2.0944rad)
  Support = -> [YZ_Plane769]
  sketch-geometry (1):
    g0: LineSegment StartX=0 StartY=0 StartZ=0 EndX=0 EndY=190 EndZ=0
  constraints (3):
    c: Coincident(g0,g-1)
    c: Vertical(g0)
    c: DistanceY(g0,g0) = 190
FEATURE [Sketcher::SketchObject] Sketch1997
  MapMode = 5
  Placement = pos=(0,0,3) rot=(0,0,1;0rad)
  Support = -> [Pad834]
  sketch-geometry (1):
    g0: Circle CenterX=0 CenterY=0 CenterZ=0 NormalX=0 NormalY=0 NormalZ=1 AngleXU=0 Radius=1.5
  constraints (2):
    c: Coincident(g0,g-1)
    c: Radius(g0) = 1.5
FEATURE [PartDesign::Pad] Pad831  label="M3x8 Thread101"
  BaseFeature = -> Pad834
  Length = 8
  Length2 = 100
  Profile = -> Sketch1997
  Type = 0
FEATURE [Sketcher::SketchObject] Sketch1992
  MapMode = 5
  Placement = pos=(0,0,0) rot=(1,0,0;3.14159rad)
  Support = -> [Pad831]
  sketch-geometry (7):
    g0: LineSegment StartX=1.275 StartY=0.736122 StartZ=0 EndX=0 EndY=1.47224 EndZ=0
    g1: LineSegment StartX=0 StartY=1.47224 StartZ=0 EndX=-1.275 EndY=0.736122 EndZ=0
    g2: LineSegment StartX=-1.275 StartY=0.736122 StartZ=0 EndX=-1.275 EndY=-0.736122 EndZ=0
    g3: LineSegment StartX=-1.275 StartY=-0.736122 StartZ=0 EndX=1.34766e-11 EndY=-1.47224 EndZ=0
    g4: LineSegment StartX=1.34766e-11 StartY=-1.47224 StartZ=0 EndX=1.275 EndY=-0.736122 EndZ=0
    g5: LineSegment StartX=1.275 StartY=-0.736122 StartZ=0 EndX=1.275 EndY=0.736122 EndZ=0
    g6: Circle [constr] CenterX=0 CenterY=0 CenterZ=0 NormalX=0 NormalY=0 NormalZ=1 AngleXU=0 Radius=1.47224
  constraints (16):
    c: Coincident(g0,g1)
    c: Coincident(g1,g2)
    c: Coincident(g2,g3)
    c: Coincident(g3,g4)
    c: Coincident(g4,g5)
    c: Coincident(g5,g0)
    c: Equal(g0, g1-g5) x5
    c: PointOnObject(g0,g6)
    c: PointOnObject(g1,g6)
    c: PointOnObject(g2,g6)
    c: PointOnObject(g3,g6)
    c: PointOnObject(g4,g6)
    c: PointOnObject(g5,g6)
    c: Coincident(g6,g-1)
    c: PointOnObject(g0,g-2)
    c: DistanceX(g1,g0) = 2.55
FEATURE [PartDesign::Pocket] Pocket710  label="M3x8 Wrench102"
  BaseFeature = -> Pad831
  Length = 1.3
  Length2 = 100
  Profile = -> Sketch1992
  Type = 0
FEATURE [PartDesign::Chamfer] Chamfer390  label="M3x8 Smooth100"
  Base = -> Pocket710 [Face11,Edge2,Edge24,Edge3]
  BaseFeature = -> Pocket710
  Size = 0.2
FEATURE [PartDesign::Body] Body537  label="M3x114"
  Group = -> [Sketch1977,Pad834,Sketch1997,Pad831,Sketch1992,Pocket710,Chamfer390]
  Origin = -> Origin750
  Placement = pos=(14.15,-14.15,-6) rot=(0,0,1;0rad)
  Tip = -> Chamfer390
FEATURE [Sketcher::SketchObject] Sketch1998
  MapMode = 5
  Placement = pos=(0,0,3) rot=(0,0,1;0rad)
  Support = -> [Pad855]
  sketch-geometry (1):
    g0: Circle CenterX=0 CenterY=0 CenterZ=0 NormalX=0 NormalY=0 NormalZ=1 AngleXU=0 Radius=1.5
  constraints (2):
    c: Coincident(g0,g-1)
    c: Radius(g0) = 1.5
FEATURE [PartDesign::Pad] Pad865  label="M3x8 Thread111"
  BaseFeature = -> Pad855
  Length = 8
  Length2 = 100
  Profile = -> Sketch1998
  Type = 0
FEATURE [Sketcher::SketchObject] Sketch1982
  MapMode = 5
  Placement = pos=(0,0,0) rot=(1,0,0;3.14159rad)
  Support = -> [Pad865]
  sketch-geometry (7):
    g0: LineSegment StartX=1.275 StartY=0.736122 StartZ=0 EndX=0 EndY=1.47224 EndZ=0
    g1: LineSegment StartX=0 StartY=1.47224 StartZ=0 EndX=-1.275 EndY=0.736122 EndZ=0
    g2: LineSegment StartX=-1.275 StartY=0.736122 StartZ=0 EndX=-1.275 EndY=-0.736122 EndZ=0
    g3: LineSegment StartX=-1.275 StartY=-0.736122 StartZ=0 EndX=1.34766e-11 EndY=-1.47224 EndZ=0
    g4: LineSegment StartX=1.34766e-11 StartY=-1.47224 StartZ=0 EndX=1.275 EndY=-0.736122 EndZ=0
    g5: LineSegment StartX=1.275 StartY=-0.736122 StartZ=0 EndX=1.275 EndY=0.736122 EndZ=0
    g6: Circle [constr] CenterX=0 CenterY=0 CenterZ=0 NormalX=0 NormalY=0 NormalZ=1 AngleXU=0 Radius=1.47224
  constraints (16):
    c: Coincident(g0,g1)
    c: Coincident(g1,g2)
    c: Coincident(g2,g3)
    c: Coincident(g3,g4)
    c: Coincident(g4,g5)
    c: Coincident(g5,g0)
    c: Equal(g0, g1-g5) x5
    c: PointOnObject(g0,g6)
    c: PointOnObject(g1,g6)
    c: PointOnObject(g2,g6)
    c: PointOnObject(g3,g6)
    c: PointOnObject(g4,g6)
    c: PointOnObject(g5,g6)
    c: Coincident(g6,g-1)
    c: PointOnObject(g0,g-2)
    c: DistanceX(g1,g0) = 2.55
FEATURE [PartDesign::Pocket] Pocket721  label="M3x8 Wrench110"
  BaseFeature = -> Pad865
  Length = 1.3
  Length2 = 100
  Profile = -> Sketch1982
  Type = 0
FEATURE [PartDesign::Chamfer] Chamfer409  label="M3x8 Smooth110"
  Base = -> Pocket721 [Face11,Edge2,Edge24,Edge3]
  BaseFeature = -> Pocket721
  Size = 0.2
FEATURE [PartDesign::Body] Body539  label="M3x115"
  Group = -> [Sketch1984,Pad855,Sketch1998,Pad865,Sketch1982,Pocket721,Chamfer409]
  Origin = -> Origin762
  Placement = pos=(-14.15,14.15,-6) rot=(0,0,1;0rad)
  Tip = -> Chamfer409
FEATURE [App::Part] Part216  label="Shouldercap Screws003"
  Group = -> [Body529,Body537,Body539,Body532]
  Origin = -> Origin757
FEATURE [Sketcher::SketchObject] Sketch1999
  ExternalGeometry = -> [Pad845]
  MapMode = 5
  Placement = pos=(0,0,0) rot=(0.57735,0.57735,0.57735;2.0944rad)
  Support = -> [YZ_Plane765]
  sketch-geometry (6):
    g0: LineSegment StartX=-1.9594 StartY=0.6 StartZ=0 EndX=-2.8094 EndY=0.6 EndZ=0
    g1: LineSegment StartX=-2.8094 StartY=0.6 StartZ=0 EndX=-2.8094 EndY=-0.6 EndZ=0
    g2: LineSegment StartX=-2.8094 StartY=-0.6 StartZ=0 EndX=-1.9594 EndY=-0.6 EndZ=0
    g3: LineSegment StartX=-1.9594 StartY=-0.6 StartZ=0 EndX=-2.3094 EndY=-0.4 EndZ=0
    g4: LineSegment StartX=-2.3094 StartY=-0.4 StartZ=0 EndX=-2.3094 EndY=0.4 EndZ=0
    g5: LineSegment StartX=-2.3094 StartY=0.4 StartZ=0 EndX=-1.9594 EndY=0.6 EndZ=0
  constraints (15):
    c: Horizontal(g0)
    c: Coincident(g0,g1)
    c: Coincident(g1,g2)
    c: Coincident(g2,g3)
    c: Coincident(g3,g4)
    c: Coincident(g4,g5)
    c: Coincident(g5,g0)
    c: Symmetric(g4,g3,g-1)
    c: Symmetric(g0,g2,g-1)
    c: Symmetric(g1,g0,g-1)
    c: DistanceX(g0,g4) = 0.5
    c: DistanceY(g3,g4) = 0.8
    c: DistanceY(g1,g0) = 1.2
    c: PointOnObject(g3,g-3)
    c: DistanceX(g4,g0) = 0.35
FEATURE [PartDesign::Groove] Groove173  label="M3 Nut Smooth165"
  Angle = 360
  Axis = (-2e-16,3e-16,1)
  Base = (0,0,0)
  BaseFeature = -> Pad845
  Profile = -> Sketch1999
  ReferenceAxis = -> Sketch1999 [V_Axis]
  Reversed = true
FEATURE [PartDesign::Chamfer] Chamfer395  label="M3 Nut Smooth Hole165"
  Base = -> Groove173 [Edge24,Edge23]
  BaseFeature = -> Groove173
  Size = 0.2
FEATURE [PartDesign::Body] Body533  label="M2 Nut063"
  Group = -> [Sketch1934,Pad845,Sketch1999,Groove173,Chamfer395,Sketch1906,Sketch1907]
  Origin = -> Origin739
  Placement = pos=(0,0,2.75) rot=(0,0,1;0rad)
  Tip = -> Chamfer395
FEATURE [App::Part] Part207  label="M063"
  Group = -> [Body536,Body533]
  Origin = -> Origin748
  Placement = pos=(-9.8e-15,10.5,80) rot=(0,1,0;3.14159rad)
FEATURE [App::Part] Part211  label="Screws014"
  Group = -> [Part207,Part214,Part206,Part212,Part217,Part215]
  Origin = -> Origin745
  Placement = pos=(0,0,-71) rot=(0,0,1;0rad)
FEATURE [App::Part] Part209  label="Shoulderjoint CAP003"
  Group = -> [Part211,Part208,Body541]
  Origin = -> Origin766
  Placement = pos=(0,0,-12) rot=(0,0,1;0rad)
FEATURE [Sketcher::SketchObject] Sketch2000
  MapMode = 5
  Support = -> [XY_Plane766]
  sketch-geometry (1):
    g0: Circle CenterX=0 CenterY=0 CenterZ=0 NormalX=0 NormalY=0 NormalZ=1 AngleXU=0 Radius=2.75
  constraints (2):
    c: Coincident(g0,g-1)
    c: Radius(g0) = 2.75
FEATURE [PartDesign::Pad] Pad871  label="M3x8 Head112"
  Length = 3
  Length2 = 100
  Profile = -> Sketch2000
  Type = 0
FEATURE [Sketcher::SketchObject] Sketch1994
  MapMode = 5
  Placement = pos=(0,0,3) rot=(0,0,1;0rad)
  Support = -> [Pad871]
  sketch-geometry (1):
    g0: Circle CenterX=0 CenterY=0 CenterZ=0 NormalX=0 NormalY=0 NormalZ=1 AngleXU=0 Radius=1.5
  constraints (2):
    c: Coincident(g0,g-1)
    c: Radius(g0) = 1.5
FEATURE [PartDesign::Pad] Pad870  label="M3x8 Thread112"
  BaseFeature = -> Pad871
  Length = 8
  Length2 = 100
  Profile = -> Sketch1994
  Type = 0
FEATURE [Sketcher::SketchObject] Sketch2001
  MapMode = 5
  Placement = pos=(0,0,0) rot=(1,0,0;3.14159rad)
  Support = -> [Pad870]
  sketch-geometry (7):
    g0: LineSegment StartX=1.275 StartY=0.736122 StartZ=0 EndX=0 EndY=1.47224 EndZ=0
    g1: LineSegment StartX=0 StartY=1.47224 StartZ=0 EndX=-1.275 EndY=0.736122 EndZ=0
    g2: LineSegment StartX=-1.275 StartY=0.736122 StartZ=0 EndX=-1.275 EndY=-0.736122 EndZ=0
    g3: LineSegment StartX=-1.275 StartY=-0.736122 StartZ=0 EndX=1.34766e-11 EndY=-1.47224 EndZ=0
    g4: LineSegment StartX=1.34766e-11 StartY=-1.47224 StartZ=0 EndX=1.275 EndY=-0.736122 EndZ=0
    g5: LineSegment StartX=1.275 StartY=-0.736122 StartZ=0 EndX=1.275 EndY=0.736122 EndZ=0
    g6: Circle [constr] CenterX=0 CenterY=0 CenterZ=0 NormalX=0 NormalY=0 NormalZ=1 AngleXU=0 Radius=1.47224
  constraints (16):
    c: Coincident(g0,g1)
    c: Coincident(g1,g2)
    c: Coincident(g2,g3)
    c: Coincident(g3,g4)
    c: Coincident(g4,g5)
    c: Coincident(g5,g0)
    c: Equal(g0, g1-g5) x5
    c: PointOnObject(g0,g6)
    c: PointOnObject(g1,g6)
    c: PointOnObject(g2,g6)
    c: PointOnObject(g3,g6)
    c: PointOnObject(g4,g6)
    c: PointOnObject(g5,g6)
    c: Coincident(g6,g-1)
    c: PointOnObject(g0,g-2)
    c: DistanceX(g1,g0) = 2.55
FEATURE [PartDesign::Pocket] Pocket735  label="M3x8 Wrench112"
  BaseFeature = -> Pad870
  Length = 1.3
  Length2 = 100
  Profile = -> Sketch2001
  Type = 0
FEATURE [PartDesign::Chamfer] Chamfer392  label="M3x8 Smooth101"
  Base = -> Pocket735 [Face11,Edge2,Edge24,Edge3]
  BaseFeature = -> Pocket735
  Size = 0.2
FEATURE [PartDesign::Body] Body544  label="M3x116"
  Group = -> [Sketch2000,Pad871,Sketch1994,Pad870,Sketch2001,Pocket735,Chamfer392,Sketch1996]
  Origin = -> Origin770
  Placement = pos=(-5.2,-40,200.6) rot=(-1,0,0;1.5708rad)
  Tip = -> Chamfer392
FEATURE [App::Part] Part213  label="FL Shoulder Joint001"
  Group = -> [Body542,Part209,Part210,Part218,Part216,Body544]
  Origin = -> Origin756
  Placement = pos=(-5.2,45.65,200.6) rot=(0,0.707107,0.707107;3.14159rad)
FEATURE [Sketcher::SketchObject] Sketch2014
  MapMode = 5
  Placement = pos=(0,0,0) rot=(1,0,0;1.5708rad)
  Support = -> [XZ_Plane778]
  sketch-geometry (1):
    g0: Circle CenterX=0 CenterY=4 CenterZ=0 NormalX=0 NormalY=0 NormalZ=1 AngleXU=0 Radius=0.75
  constraints (3):
    c: PointOnObject(g0,g-2)
    c: Radius(g0) = 0.75
    c: DistanceY(g-1,g0) = 4
FEATURE [Sketcher::SketchObject] Sketch2015
  MapMode = 5
  Placement = pos=(0,0,0) rot=(1,0,0;1.5708rad)
  Support = -> [XZ_Plane787]
  sketch-geometry (1):
    g0: Circle CenterX=1.55 CenterY=4 CenterZ=0 NormalX=0 NormalY=0 NormalZ=1 AngleXU=0 Radius=0.75
  constraints (3):
    c: Radius(g0) = 0.75
    c: DistanceY(g-1,g0) = 4
    c: DistanceX(g-1,g0) = 1.55
FEATURE [Sketcher::SketchObject] Sketch2017
  MapMode = 5
  Support = -> [XY_Plane787]
  sketch-geometry (4):
    g0: LineSegment StartX=-10 StartY=20.15 StartZ=0 EndX=10 EndY=20.15 EndZ=0
    g1: LineSegment StartX=10 StartY=20.15 StartZ=0 EndX=10 EndY=-20.15 EndZ=0
    g2: LineSegment StartX=10 StartY=-20.15 StartZ=0 EndX=-10 EndY=-20.15 EndZ=0
    g3: LineSegment StartX=-10 StartY=-20.15 StartZ=0 EndX=-10 EndY=20.15 EndZ=0
  constraints (10):
    c: Coincident(g0,g1)
    c: Coincident(g1,g2)
    c: Coincident(g2,g3)
    c: Coincident(g3,g0)
    c: Horizontal(g2)
    c: Vertical(g3)
    c: DistanceX(g0,g0) = 20
    c: DistanceY(g1,g1) = 40.3
    c: Symmetric(g0,g1,g-1)
    c: Symmetric(g0,g0,g-2)
FEATURE [Sketcher::SketchObject] Sketch2022
  MapMode = 5
  Support = -> [XY_Plane779]
  sketch-geometry (8):
    g0: LineSegment StartX=0 StartY=3.17543 StartZ=0 EndX=-2.75 EndY=1.58771 EndZ=0
    g1: LineSegment StartX=-2.75 StartY=1.58771 StartZ=0 EndX=-2.75 EndY=-1.58771 EndZ=0
    g2: LineSegment StartX=-2.75 StartY=-1.58771 StartZ=0 EndX=0 EndY=-3.17543 EndZ=0
    g3: LineSegment StartX=0 StartY=-3.17543 StartZ=0 EndX=2.75 EndY=-1.58771 EndZ=0
    g4: LineSegment StartX=2.75 StartY=-1.58771 StartZ=0 EndX=2.75 EndY=1.58771 EndZ=0
    g5: LineSegment StartX=2.75 StartY=1.58771 StartZ=0 EndX=0 EndY=3.17543 EndZ=0
    g6: Circle [constr] CenterX=0 CenterY=0 CenterZ=0 NormalX=0 NormalY=0 NormalZ=1 AngleXU=0 Radius=3.17543
    g7: Circle CenterX=0 CenterY=0 CenterZ=0 NormalX=0 NormalY=0 NormalZ=1 AngleXU=0 Radius=1.5
  constraints (18):
    c: Coincident(g0,g1)
    c: Coincident(g1,g2)
    c: Coincident(g2,g3)
    c: Coincident(g3,g4)
    c: Coincident(g4,g5)
    c: Coincident(g5,g0)
    c: Equal(g0, g1-g5) x5
    c: PointOnObject(g0,g6)
    c: PointOnObject(g1,g6)
    c: PointOnObject(g2,g6)
    c: PointOnObject(g3,g6)
    c: PointOnObject(g4,g6)
    c: PointOnObject(g5,g6)
    c: Coincident(g6,g-1)
    c: PointOnObject(g5,g-2)
    c: DistanceX(g0,g4) = 5.5
    c: Coincident(g7,g-1)
    c: Radius(g7) = 1.5
FEATURE [Sketcher::SketchObject] Sketch2024
  MapMode = 5
  Placement = pos=(0,0,0) rot=(1,0,0;1.5708rad)
  Support = -> [XZ_Plane786]
  sketch-geometry (1):
    g0: Circle CenterX=-1.55 CenterY=4 CenterZ=0 NormalX=0 NormalY=0 NormalZ=1 AngleXU=0 Radius=0.75
  constraints (3):
    c: Radius(g0) = 0.75
    c: DistanceY(g-1,g0) = 4
    c: DistanceX(g0,g-1) = 1.55
FEATURE [PartDesign::Pad] Pad874
  Length = 10
  Length2 = 100
  Placement = pos=(0,0,0) rot=(1,0,0;1.5708rad)
  Profile = -> Sketch2024
  Reversed = true
  Type = 0
FEATURE [PartDesign::Body] Body557  label="orange wire015"
  Group = -> [Sketch2024,Pad874]
  Origin = -> Origin783
  Placement = pos=(0,25.15,0) rot=(0,0,1;0rad)
  Tip = -> Pad874
FEATURE [Sketcher::SketchObject] Sketch2025
  MapMode = 5
  Support = -> [XY_Plane781]
  sketch-geometry (1):
    g0: Circle CenterX=0 CenterY=0 CenterZ=0 NormalX=0 NormalY=0 NormalZ=1 AngleXU=0 Radius=2.75
  constraints (2):
    c: Coincident(g0,g-1)
    c: Radius(g0) = 2.75
FEATURE [Sketcher::SketchObject] Sketch2026
  MapMode = 5
  Support = -> [XY_Plane791]
  sketch-geometry (1):
    g0: Circle CenterX=0 CenterY=10.15 CenterZ=0 NormalX=0 NormalY=0 NormalZ=1 AngleXU=0 Radius=3
  constraints (3):
    c: PointOnObject(g0,g-2)
    c: DistanceY(g-1,g0) = 10.15
    c: Radius(g0) = 3
FEATURE [PartDesign::Pad] Pad875
  Length = 5
  Length2 = 100
  Profile = -> Sketch2026
  Type = 0
FEATURE [Sketcher::SketchObject] Sketch2012
  ExternalGeometry = -> [Pad875]
  MapMode = 5
  Placement = pos=(0,0,5) rot=(0,0,1;0rad)
  Support = -> [Pad875]
  sketch-geometry (1):
    g0: Circle CenterX=0 CenterY=10.15 CenterZ=0 NormalX=0 NormalY=0 NormalZ=1 AngleXU=0 Radius=1.5
  constraints (2):
    c: Coincident(g0,g-3)
    c: Radius(g0) = 1.5
FEATURE [PartDesign::Pocket] Pocket739
  BaseFeature = -> Pad875
  Length = 4
  Length2 = 100
  Profile = -> Sketch2012
  Type = 0
FEATURE [PartDesign::Chamfer] Chamfer419
  Base = -> Pocket739 [Edge3]
  BaseFeature = -> Pocket739
  Size = 0.25
FEATURE [PartDesign::Body] Body561  label="Gear014"
  Group = -> [Sketch2026,Pad875,Sketch2012,Pocket739,Chamfer419]
  Origin = -> Origin785
  Placement = pos=(0,0,38.25) rot=(0,0,1;0rad)
  Tip = -> Chamfer419
FEATURE [Sketcher::SketchObject] Sketch2028
  MapMode = 5
  Support = -> [XY_Plane782]
  sketch-geometry (8):
    g0: LineSegment StartX=0 StartY=3.17543 StartZ=0 EndX=-2.75 EndY=1.58771 EndZ=0
    g1: LineSegment StartX=-2.75 StartY=1.58771 StartZ=0 EndX=-2.75 EndY=-1.58771 EndZ=0
    g2: LineSegment StartX=-2.75 StartY=-1.58771 StartZ=0 EndX=0 EndY=-3.17543 EndZ=0
    g3: LineSegment StartX=0 StartY=-3.17543 StartZ=0 EndX=2.75 EndY=-1.58771 EndZ=0
    g4: LineSegment StartX=2.75 StartY=-1.58771 StartZ=0 EndX=2.75 EndY=1.58771 EndZ=0
    g5: LineSegment StartX=2.75 StartY=1.58771 StartZ=0 EndX=0 EndY=3.17543 EndZ=0
    g6: Circle [constr] CenterX=0 CenterY=0 CenterZ=0 NormalX=0 NormalY=0 NormalZ=1 AngleXU=0 Radius=3.17543
    g7: Circle CenterX=0 CenterY=0 CenterZ=0 NormalX=0 NormalY=0 NormalZ=1 AngleXU=0 Radius=1.5
  constraints (18):
    c: Coincident(g0,g1)
    c: Coincident(g1,g2)
    c: Coincident(g2,g3)
    c: Coincident(g3,g4)
    c: Coincident(g4,g5)
    c: Coincident(g5,g0)
    c: Equal(g0, g1-g5) x5
    c: PointOnObject(g0,g6)
    c: PointOnObject(g1,g6)
    c: PointOnObject(g2,g6)
    c: PointOnObject(g3,g6)
    c: PointOnObject(g4,g6)
    c: PointOnObject(g5,g6)
    c: Coincident(g6,g-1)
    c: PointOnObject(g5,g-2)
    c: DistanceX(g0,g4) = 5.5
    c: Coincident(g7,g-1)
    c: Radius(g7) = 1.5
FEATURE [Sketcher::SketchObject] Sketch2029
  MapMode = 5
  Support = -> [XY_Plane780]
  sketch-geometry (8):
    g0: LineSegment StartX=0 StartY=3.17543 StartZ=0 EndX=-2.75 EndY=1.58771 EndZ=0
    g1: LineSegment StartX=-2.75 StartY=1.58771 StartZ=0 EndX=-2.75 EndY=-1.58771 EndZ=0
    g2: LineSegment StartX=-2.75 StartY=-1.58771 StartZ=0 EndX=0 EndY=-3.17543 EndZ=0
    g3: LineSegment StartX=0 StartY=-3.17543 StartZ=0 EndX=2.75 EndY=-1.58771 EndZ=0
    g4: LineSegment StartX=2.75 StartY=-1.58771 StartZ=0 EndX=2.75 EndY=1.58771 EndZ=0
    g5: LineSegment StartX=2.75 StartY=1.58771 StartZ=0 EndX=0 EndY=3.17543 EndZ=0
    g6: Circle [constr] CenterX=0 CenterY=0 CenterZ=0 NormalX=0 NormalY=0 NormalZ=1 AngleXU=0 Radius=3.17543
    g7: Circle CenterX=0 CenterY=0 CenterZ=0 NormalX=0 NormalY=0 NormalZ=1 AngleXU=0 Radius=1.5
  constraints (18):
    c: Coincident(g0,g1)
    c: Coincident(g1,g2)
    c: Coincident(g2,g3)
    c: Coincident(g3,g4)
    c: Coincident(g4,g5)
    c: Coincident(g5,g0)
    c: Equal(g0, g1-g5) x5
    c: PointOnObject(g0,g6)
    c: PointOnObject(g1,g6)
    c: PointOnObject(g2,g6)
    c: PointOnObject(g3,g6)
    c: PointOnObject(g4,g6)
    c: PointOnObject(g5,g6)
    c: Coincident(g6,g-1)
    c: PointOnObject(g5,g-2)
    c: DistanceX(g0,g4) = 5.5
    c: Coincident(g7,g-1)
    c: Radius(g7) = 1.5
FEATURE [Sketcher::SketchObject] Sketch2030
  MapMode = 5
  Support = -> [XY_Plane783]
  sketch-geometry (8):
    g0: LineSegment StartX=0 StartY=3.17543 StartZ=0 EndX=-2.75 EndY=1.58771 EndZ=0
    g1: LineSegment StartX=-2.75 StartY=1.58771 StartZ=0 EndX=-2.75 EndY=-1.58771 EndZ=0
    g2: LineSegment StartX=-2.75 StartY=-1.58771 StartZ=0 EndX=0 EndY=-3.17543 EndZ=0
    g3: LineSegment StartX=0 StartY=-3.17543 StartZ=0 EndX=2.75 EndY=-1.58771 EndZ=0
    g4: LineSegment StartX=2.75 StartY=-1.58771 StartZ=0 EndX=2.75 EndY=1.58771 EndZ=0
    g5: LineSegment StartX=2.75 StartY=1.58771 StartZ=0 EndX=0 EndY=3.17543 EndZ=0
    g6: Circle [constr] CenterX=0 CenterY=0 CenterZ=0 NormalX=0 NormalY=0 NormalZ=1 AngleXU=0 Radius=3.17543
    g7: Circle CenterX=0 CenterY=0 CenterZ=0 NormalX=0 NormalY=0 NormalZ=1 AngleXU=0 Radius=1.5
  constraints (18):
    c: Coincident(g0,g1)
    c: Coincident(g1,g2)
    c: Coincident(g2,g3)
    c: Coincident(g3,g4)
    c: Coincident(g4,g5)
    c: Coincident(g5,g0)
    c: Equal(g0, g1-g5) x5
    c: PointOnObject(g0,g6)
    c: PointOnObject(g1,g6)
    c: PointOnObject(g2,g6)
    c: PointOnObject(g3,g6)
    c: PointOnObject(g4,g6)
    c: PointOnObject(g5,g6)
    c: Coincident(g6,g-1)
    c: PointOnObject(g5,g-2)
    c: DistanceX(g0,g4) = 5.5
    c: Coincident(g7,g-1)
    c: Radius(g7) = 1.5
FEATURE [Sketcher::SketchObject] Sketch2033
  MapMode = 5
  Support = -> [XY_Plane776]
  sketch-geometry (1):
    g0: Circle CenterX=0 CenterY=0 CenterZ=0 NormalX=0 NormalY=0 NormalZ=1 AngleXU=0 Radius=2.75
  constraints (2):
    c: Coincident(g0,g-1)
    c: Radius(g0) = 2.75
FEATURE [Sketcher::SketchObject] Sketch2038
  MapMode = 5
  Support = -> [XY_Plane785]
  sketch-geometry (1):
    g0: Circle CenterX=0 CenterY=0 CenterZ=0 NormalX=0 NormalY=0 NormalZ=1 AngleXU=0 Radius=2.75
  constraints (2):
    c: Coincident(g0,g-1)
    c: Radius(g0) = 2.75
FEATURE [Sketcher::SketchObject] Sketch2040
  MapMode = 5
  Support = -> [XY_Plane777]
  sketch-geometry (1):
    g0: Circle CenterX=0 CenterY=0 CenterZ=0 NormalX=0 NormalY=0 NormalZ=1 AngleXU=0 Radius=2.75
  constraints (2):
    c: Coincident(g0,g-1)
    c: Radius(g0) = 2.75
FEATURE [PartDesign::Pad] Pad878
  Length = 10
  Length2 = 100
  Placement = pos=(0,0,0) rot=(1,0,0;1.5708rad)
  Profile = -> Sketch2014
  Reversed = true
  Type = 0
FEATURE [PartDesign::Body] Body560  label="red wire014"
  Group = -> [Sketch2014,Pad878]
  Origin = -> Origin788
  Placement = pos=(0,25.15,0) rot=(0,0,1;0rad)
  Tip = -> Pad878
FEATURE [PartDesign::Pad] Pad881  label="M3 Nut Primitive175"
  Length = 1.2
  Length2 = 1.2
  Profile = -> Sketch2030
  Type = 4
FEATURE [Sketcher::SketchObject] Sketch2031
  ExternalGeometry = -> [Pad881]
  MapMode = 5
  Placement = pos=(0,0,0) rot=(0.57735,0.57735,0.57735;2.0944rad)
  Support = -> [YZ_Plane772]
  sketch-geometry (6):
    g0: LineSegment StartX=-2.67543 StartY=1.2 StartZ=0 EndX=-3.67543 EndY=1.2 EndZ=0
    g1: LineSegment StartX=-3.67543 StartY=1.2 StartZ=0 EndX=-3.67543 EndY=-1.2 EndZ=0
    g2: LineSegment StartX=-3.67543 StartY=-1.2 StartZ=0 EndX=-2.67543 EndY=-1.2 EndZ=0
    g3: LineSegment StartX=-2.67543 StartY=-1.2 StartZ=0 EndX=-3.17543 EndY=-1 EndZ=0
    g4: LineSegment StartX=-3.17543 StartY=-1 StartZ=0 EndX=-3.17543 EndY=1 EndZ=0
    g5: LineSegment StartX=-3.17543 StartY=1 StartZ=0 EndX=-2.67543 EndY=1.2 EndZ=0
  constraints (15):
    c: Horizontal(g0)
    c: Coincident(g0,g1)
    c: Coincident(g1,g2)
    c: Coincident(g2,g3)
    c: Coincident(g3,g4)
    c: Coincident(g4,g5)
    c: Coincident(g5,g0)
    c: Symmetric(g4,g3,g-1)
    c: Symmetric(g0,g2,g-1)
    c: Symmetric(g1,g0,g-1)
    c: DistanceX(g0,g4) = 0.5
    c: DistanceY(g3,g4) = 2
    c: DistanceY(g1,g0) = 2.4
    c: PointOnObject(g3,g-3)
    c: DistanceX(g4,g0) = 0.5
FEATURE [PartDesign::Pad] Pad883  label="M3 Nut Primitive176"
  Length = 1.2
  Length2 = 1.2
  Profile = -> Sketch2029
  Type = 4
FEATURE [Sketcher::SketchObject] Sketch2018
  ExternalGeometry = -> [Pad883]
  MapMode = 5
  Placement = pos=(0,0,0) rot=(0.57735,0.57735,0.57735;2.0944rad)
  Support = -> [YZ_Plane776]
  sketch-geometry (6):
    g0: LineSegment StartX=-2.67543 StartY=1.2 StartZ=0 EndX=-3.67543 EndY=1.2 EndZ=0
    g1: LineSegment StartX=-3.67543 StartY=1.2 StartZ=0 EndX=-3.67543 EndY=-1.2 EndZ=0
    g2: LineSegment StartX=-3.67543 StartY=-1.2 StartZ=0 EndX=-2.67543 EndY=-1.2 EndZ=0
    g3: LineSegment StartX=-2.67543 StartY=-1.2 StartZ=0 EndX=-3.17543 EndY=-1 EndZ=0
    g4: LineSegment StartX=-3.17543 StartY=-1 StartZ=0 EndX=-3.17543 EndY=1 EndZ=0
    g5: LineSegment StartX=-3.17543 StartY=1 StartZ=0 EndX=-2.67543 EndY=1.2 EndZ=0
  constraints (15):
    c: Horizontal(g0)
    c: Coincident(g0,g1)
    c: Coincident(g1,g2)
    c: Coincident(g2,g3)
    c: Coincident(g3,g4)
    c: Coincident(g4,g5)
    c: Coincident(g5,g0)
    c: Symmetric(g4,g3,g-1)
    c: Symmetric(g0,g2,g-1)
    c: Symmetric(g1,g0,g-1)
    c: DistanceX(g0,g4) = 0.5
    c: DistanceY(g3,g4) = 2
    c: DistanceY(g1,g0) = 2.4
    c: PointOnObject(g3,g-3)
    c: DistanceX(g4,g0) = 0.5
FEATURE [PartDesign::Groove] Groove183  label="M3 Nut Smooth175"
  Angle = 360
  Axis = (-2e-16,3e-16,1)
  Base = (0,0,0)
  BaseFeature = -> Pad883
  Profile = -> Sketch2018
  ReferenceAxis = -> Sketch2018 [V_Axis]
  Reversed = true
FEATURE [PartDesign::Chamfer] Chamfer420  label="M3 Nut Smooth Hole178"
  Base = -> Groove183 [Edge24,Edge23]
  BaseFeature = -> Groove183
  Size = 0.2
FEATURE [PartDesign::Body] Body566  label="M3 Nut102"
  Group = -> [Sketch2029,Pad883,Sketch2018,Groove183,Chamfer420]
  Origin = -> Origin779
  Placement = pos=(1.5e-14,-55.6,176.35) rot=(0.57735,-0.57735,0.57735;4.18879rad)
  Tip = -> Chamfer420
FEATURE [PartDesign::Pad] Pad886  label="M3 Nut Primitive177"
  Length = 1.2
  Length2 = 1.2
  Profile = -> Sketch2028
  Type = 4
FEATURE [Sketcher::SketchObject] Sketch2020
  ExternalGeometry = -> [Pad886]
  MapMode = 5
  Placement = pos=(0,0,0) rot=(0.57735,0.57735,0.57735;2.0944rad)
  Support = -> [YZ_Plane771]
  sketch-geometry (6):
    g0: LineSegment StartX=-2.67543 StartY=1.2 StartZ=0 EndX=-3.67543 EndY=1.2 EndZ=0
    g1: LineSegment StartX=-3.67543 StartY=1.2 StartZ=0 EndX=-3.67543 EndY=-1.2 EndZ=0
    g2: LineSegment StartX=-3.67543 StartY=-1.2 StartZ=0 EndX=-2.67543 EndY=-1.2 EndZ=0
    g3: LineSegment StartX=-2.67543 StartY=-1.2 StartZ=0 EndX=-3.17543 EndY=-1 EndZ=0
    g4: LineSegment StartX=-3.17543 StartY=-1 StartZ=0 EndX=-3.17543 EndY=1 EndZ=0
    g5: LineSegment StartX=-3.17543 StartY=1 StartZ=0 EndX=-2.67543 EndY=1.2 EndZ=0
  constraints (15):
    c: Horizontal(g0)
    c: Coincident(g0,g1)
    c: Coincident(g1,g2)
    c: Coincident(g2,g3)
    c: Coincident(g3,g4)
    c: Coincident(g4,g5)
    c: Coincident(g5,g0)
    c: Symmetric(g4,g3,g-1)
    c: Symmetric(g0,g2,g-1)
    c: Symmetric(g1,g0,g-1)
    c: DistanceX(g0,g4) = 0.5
    c: DistanceY(g3,g4) = 2
    c: DistanceY(g1,g0) = 2.4
    c: PointOnObject(g3,g-3)
    c: DistanceX(g4,g0) = 0.5
FEATURE [PartDesign::Pad] Pad888
  Length = 10
  Length2 = 100
  Placement = pos=(0,0,0) rot=(1,0,0;1.5708rad)
  Profile = -> Sketch2015
  Reversed = true
  Type = 0
FEATURE [PartDesign::Body] Body559  label="brown wire014"
  Group = -> [Sketch2015,Pad888]
  Origin = -> Origin780
  Placement = pos=(0,25.15,0) rot=(0,0,1;0rad)
  Tip = -> Pad888
FEATURE [PartDesign::Pad] Pad890  label="Baseblock018"
  Length = 26.6
  Length2 = 100
  Profile = -> Sketch2017
  Type = 0
FEATURE [Sketcher::SketchObject] Sketch2008
  MapMode = 5
  Placement = pos=(0,0,26.6) rot=(0,0,1;0rad)
  Support = -> [Pad890]
  sketch-geometry (4):
    g0: LineSegment StartX=-10 StartY=-26.8 StartZ=0 EndX=10 EndY=-26.8 EndZ=0
    g1: LineSegment StartX=10 StartY=-26.8 StartZ=0 EndX=10 EndY=26.8 EndZ=0
    g2: LineSegment StartX=10 StartY=26.8 StartZ=0 EndX=-10 EndY=26.8 EndZ=0
    g3: LineSegment StartX=-10 StartY=26.8 StartZ=0 EndX=-10 EndY=-26.8 EndZ=0
  constraints (10):
    c: Coincident(g0,g1)
    c: Coincident(g1,g2)
    c: Coincident(g2,g3)
    c: Coincident(g3,g0)
    c: Horizontal(g0)
    c: Vertical(g3)
    c: Symmetric(g1,g2,g-2)
    c: Symmetric(g1,g0,g-1)
    c: DistanceX(g2,g2) = 20
    c: DistanceY(g1,g1) = 53.6
FEATURE [PartDesign::Pad] Pad887
  BaseFeature = -> Pad890
  Length = 2.5
  Length2 = 100
  Profile = -> Sketch2008
  Type = 0
FEATURE [Sketcher::SketchObject] Sketch2006
  MapMode = 5
  Placement = pos=(0,0,29.1) rot=(0,0,1;0rad)
  Support = -> [Pad887]
  sketch-geometry (4):
    g0: LineSegment StartX=-10 StartY=-20.15 StartZ=0 EndX=10 EndY=-20.15 EndZ=0
    g1: LineSegment StartX=10 StartY=-20.15 StartZ=0 EndX=10 EndY=20.15 EndZ=0
    g2: LineSegment StartX=10 StartY=20.15 StartZ=0 EndX=-10 EndY=20.15 EndZ=0
    g3: LineSegment StartX=-10 StartY=20.15 StartZ=0 EndX=-10 EndY=-20.15 EndZ=0
  constraints (10):
    c: Coincident(g0,g1)
    c: Coincident(g1,g2)
    c: Coincident(g2,g3)
    c: Coincident(g3,g0)
    c: Horizontal(g0)
    c: Vertical(g3)
    c: Symmetric(g1,g2,g-2)
    c: Symmetric(g1,g0,g-1)
    c: DistanceX(g2,g2) = 20
    c: DistanceY(g1,g1) = 40.3
FEATURE [PartDesign::Pad] Pad885
  BaseFeature = -> Pad887
  Length = 6
  Length2 = 100
  Profile = -> Sketch2006
  Type = 0
FEATURE [Sketcher::SketchObject] Sketch2011
  ExternalGeometry = -> [Pad885]
  MapMode = 5
  Placement = pos=(0,0,35.1) rot=(0,0,1;0rad)
  Support = -> [Pad885]
  sketch-geometry (7):
    g0: ArcOfCircle CenterX=-3e-16 CenterY=10.15 CenterZ=0 NormalX=0 NormalY=0 NormalZ=1 AngleXU=0 Radius=9.5 StartAngle=5.9573 EndAngle=9.75066
    g1: LineSegment StartX=-9 StartY=7.10862 StartZ=0 EndX=-9 EndY=-14.15 EndZ=0
    g2: LineSegment StartX=-9 StartY=-14.15 StartZ=0 EndX=-5 EndY=-14.15 EndZ=0
    g3: LineSegment StartX=5 StartY=-14.15 StartZ=0 EndX=9 EndY=-14.15 EndZ=0
    g4: LineSegment StartX=9 StartY=-14.15 StartZ=0 EndX=9 EndY=7.10862 EndZ=0
    g5: ArcOfCircle CenterX=-3e-16 CenterY=-10.4 CenterZ=0 NormalX=0 NormalY=0 NormalZ=1 AngleXU=0 Radius=6.25 StartAngle=3.78509 EndAngle=5.63968
    g6: LineSegment [constr] StartX=0 StartY=-20.15 StartZ=0 EndX=0 EndY=-16.65 EndZ=0
  constraints (22):
    c: Symmetric(g0,g0,g-2)
    c: Coincident(g1,g0)
    c: Vertical(g1)
    c: Coincident(g2,g1)
    c: Horizontal(g2)
    c: Horizontal(g3)
    c: Coincident(g4,g3)
    c: Coincident(g4,g0)
    c: Vertical(g4)
    c: Symmetric(g2,g3,g-2)
    c: Coincident(g5,g2)
    c: Coincident(g5,g3)
    c: DistanceY(g-3,g3) = 6
    c: DistanceY(g0,g-4) = 10
    c: Radius(g0) = 9.5
    c: DistanceX(g0,g0) = 18
    c: PointOnObject(g6,g-3)
    c: PointOnObject(g6,g5)
    c: Vertical(g6)
    c: DistanceY(g6,g6) = 3.5
    c: DistanceX(g2,g3) = 10
    c: PointOnObject(g6,g-2)
FEATURE [PartDesign::Pad] Pad876
  BaseFeature = -> Pad885
  Length = 2.5
  Length2 = 100
  Profile = -> Sketch2011
  Type = 0
FEATURE [Sketcher::SketchObject] Sketch2019
  ExternalGeometry = -> [Pad876]
  MapMode = 5
  Placement = pos=(0,0,37.6) rot=(0,0,1;0rad)
  Support = -> [Pad876]
  sketch-geometry (1):
    g0: Circle CenterX=-3e-16 CenterY=10.15 CenterZ=0 NormalX=0 NormalY=0 NormalZ=1 AngleXU=0 Radius=6.5
  constraints (2):
    c: Coincident(g0,g-3)
    c: Radius(g0) = 6.5
FEATURE [PartDesign::Pad] Pad891  label="M3x20 Head072"
  Length = 3
  Length2 = 100
  Profile = -> Sketch2025
  Type = 0
FEATURE [Sketcher::SketchObject] Sketch2036
  MapMode = 5
  Placement = pos=(0,0,3) rot=(0,0,1;0rad)
  Support = -> [Pad891]
  sketch-geometry (1):
    g0: Circle CenterX=0 CenterY=0 CenterZ=0 NormalX=0 NormalY=0 NormalZ=1 AngleXU=0 Radius=1.5
  constraints (2):
    c: Coincident(g0,g-1)
    c: Radius(g0) = 1.5
FEATURE [PartDesign::Pad] Pad889  label="M3x20 Thread073"
  BaseFeature = -> Pad891
  Length = 20
  Length2 = 100
  Profile = -> Sketch2036
  Type = 0
FEATURE [Sketcher::SketchObject] Sketch2035
  MapMode = 5
  Placement = pos=(0,0,0) rot=(1,0,0;3.14159rad)
  Support = -> [Pad889]
  sketch-geometry (7):
    g0: LineSegment StartX=1.275 StartY=0.736122 StartZ=0 EndX=0 EndY=1.47224 EndZ=0
    g1: LineSegment StartX=0 StartY=1.47224 StartZ=0 EndX=-1.275 EndY=0.736122 EndZ=0
    g2: LineSegment StartX=-1.275 StartY=0.736122 StartZ=0 EndX=-1.275 EndY=-0.736122 EndZ=0
    g3: LineSegment StartX=-1.275 StartY=-0.736122 StartZ=0 EndX=1.34766e-11 EndY=-1.47224 EndZ=0
    g4: LineSegment StartX=1.34766e-11 StartY=-1.47224 StartZ=0 EndX=1.275 EndY=-0.736122 EndZ=0
    g5: LineSegment StartX=1.275 StartY=-0.736122 StartZ=0 EndX=1.275 EndY=0.736122 EndZ=0
    g6: Circle [constr] CenterX=0 CenterY=0 CenterZ=0 NormalX=0 NormalY=0 NormalZ=1 AngleXU=0 Radius=1.47224
  constraints (16):
    c: Coincident(g0,g1)
    c: Coincident(g1,g2)
    c: Coincident(g2,g3)
    c: Coincident(g3,g4)
    c: Coincident(g4,g5)
    c: Coincident(g5,g0)
    c: Equal(g0, g1-g5) x5
    c: PointOnObject(g0,g6)
    c: PointOnObject(g1,g6)
    c: PointOnObject(g2,g6)
    c: PointOnObject(g3,g6)
    c: PointOnObject(g4,g6)
    c: PointOnObject(g5,g6)
    c: Coincident(g6,g-1)
    c: PointOnObject(g0,g-2)
    c: DistanceX(g1,g0) = 2.55
FEATURE [PartDesign::Pocket] Pocket743  label="M3x20 Wrench073"
  BaseFeature = -> Pad889
  Length = 1.3
  Length2 = 100
  Profile = -> Sketch2035
  Type = 0
FEATURE [PartDesign::Chamfer] Chamfer418  label="M3x20 Smooth071"
  Base = -> Pocket743 [Face11,Edge2,Edge24,Edge3]
  BaseFeature = -> Pocket743
  Size = 0.2
FEATURE [PartDesign::Body] Body565  label="M3x119"
  Group = -> [Sketch2025,Pad891,Sketch2036,Pad889,Sketch2035,Pocket743,Chamfer418]
  Origin = -> Origin792
  Placement = pos=(11.25,-55.6,224.85) rot=(0,-1,0;1.5708rad)
  Tip = -> Chamfer418
FEATURE [PartDesign::Groove] Groove184  label="M3 Nut Smooth176"
  Angle = 360
  Axis = (-2e-16,3e-16,1)
  Base = (0,0,0)
  BaseFeature = -> Pad881
  Profile = -> Sketch2031
  ReferenceAxis = -> Sketch2031 [V_Axis]
  Reversed = true
FEATURE [PartDesign::Chamfer] Chamfer415  label="M3 Nut Smooth Hole176"
  Base = -> Groove184 [Edge24,Edge23]
  BaseFeature = -> Groove184
  Size = 0.2
FEATURE [PartDesign::Body] Body563  label="M3 Nut101"
  Group = -> [Sketch2030,Pad881,Sketch2031,Groove184,Chamfer415]
  Origin = -> Origin782
  Placement = pos=(5e-14,-65.6,224.85) rot=(0.57735,-0.57735,0.57735;4.18879rad)
  Tip = -> Chamfer415
FEATURE [PartDesign::Groove] Groove185  label="M3 Nut Smooth177"
  Angle = 360
  Axis = (-2e-16,3e-16,1)
  Base = (0,0,0)
  BaseFeature = -> Pad886
  Profile = -> Sketch2020
  ReferenceAxis = -> Sketch2020 [V_Axis]
  Reversed = true
FEATURE [PartDesign::Chamfer] Chamfer414  label="M3 Nut Smooth Hole175"
  Base = -> Groove185 [Edge24,Edge23]
  BaseFeature = -> Groove185
  Size = 0.2
FEATURE [PartDesign::Body] Body556  label="M3 Nut100"
  Group = -> [Sketch2028,Pad886,Sketch2020,Groove185,Chamfer414]
  Origin = -> Origin791
  Placement = pos=(3.9e-14,-65.6,176.35) rot=(0.57735,-0.57735,0.57735;4.18879rad)
  Tip = -> Chamfer414
FEATURE [PartDesign::Pad] Pad892  label="M3x20 Head073"
  Length = 3
  Length2 = 100
  Profile = -> Sketch2033
  Type = 0
FEATURE [Sketcher::SketchObject] Sketch2034
  MapMode = 5
  Placement = pos=(0,0,3) rot=(0,0,1;0rad)
  Support = -> [Pad892]
  sketch-geometry (1):
    g0: Circle CenterX=0 CenterY=0 CenterZ=0 NormalX=0 NormalY=0 NormalZ=1 AngleXU=0 Radius=1.5
  constraints (2):
    c: Coincident(g0,g-1)
    c: Radius(g0) = 1.5
FEATURE [PartDesign::Pad] Pad879  label="M3x20 Thread071"
  BaseFeature = -> Pad892
  Length = 20
  Length2 = 100
  Profile = -> Sketch2034
  Type = 0
FEATURE [Sketcher::SketchObject] Sketch2032
  MapMode = 5
  Placement = pos=(0,0,0) rot=(1,0,0;3.14159rad)
  Support = -> [Pad879]
  sketch-geometry (7):
    g0: LineSegment StartX=1.275 StartY=0.736122 StartZ=0 EndX=0 EndY=1.47224 EndZ=0
    g1: LineSegment StartX=0 StartY=1.47224 StartZ=0 EndX=-1.275 EndY=0.736122 EndZ=0
    g2: LineSegment StartX=-1.275 StartY=0.736122 StartZ=0 EndX=-1.275 EndY=-0.736122 EndZ=0
    g3: LineSegment StartX=-1.275 StartY=-0.736122 StartZ=0 EndX=1.34766e-11 EndY=-1.47224 EndZ=0
    g4: LineSegment StartX=1.34766e-11 StartY=-1.47224 StartZ=0 EndX=1.275 EndY=-0.736122 EndZ=0
    g5: LineSegment StartX=1.275 StartY=-0.736122 StartZ=0 EndX=1.275 EndY=0.736122 EndZ=0
    g6: Circle [constr] CenterX=0 CenterY=0 CenterZ=0 NormalX=0 NormalY=0 NormalZ=1 AngleXU=0 Radius=1.47224
  constraints (16):
    c: Coincident(g0,g1)
    c: Coincident(g1,g2)
    c: Coincident(g2,g3)
    c: Coincident(g3,g4)
    c: Coincident(g4,g5)
    c: Coincident(g5,g0)
    c: Equal(g0, g1-g5) x5
    c: PointOnObject(g0,g6)
    c: PointOnObject(g1,g6)
    c: PointOnObject(g2,g6)
    c: PointOnObject(g3,g6)
    c: PointOnObject(g4,g6)
    c: PointOnObject(g5,g6)
    c: Coincident(g6,g-1)
    c: PointOnObject(g0,g-2)
    c: DistanceX(g1,g0) = 2.55
FEATURE [PartDesign::Pocket] Pocket742  label="M3x20 Wrench072"
  BaseFeature = -> Pad879
  Length = 1.3
  Length2 = 100
  Profile = -> Sketch2032
  Type = 0
FEATURE [PartDesign::Chamfer] Chamfer417  label="M3x20 Smooth070"
  Base = -> Pocket742 [Face11,Edge2,Edge24,Edge3]
  BaseFeature = -> Pocket742
  Size = 0.2
FEATURE [PartDesign::Body] Body562  label="M3x117"
  Group = -> [Sketch2033,Pad892,Sketch2034,Pad879,Sketch2032,Pocket742,Chamfer417]
  Origin = -> Origin778
  Placement = pos=(11.25,-65.6,224.85) rot=(0,-1,0;1.5708rad)
  Tip = -> Chamfer417
FEATURE [PartDesign::Pad] Pad893
  BaseFeature = -> Pad876
  Length = 1
  Length2 = 100
  Profile = -> Sketch2019
  Type = 0
FEATURE [Sketcher::SketchObject] Sketch2007
  ExternalGeometry = -> [Pad893]
  MapMode = 5
  Placement = pos=(0,0,38.6) rot=(0,0,1;0rad)
  Support = -> [Pad893]
  sketch-geometry (1):
    g0: Circle CenterX=0 CenterY=10.15 CenterZ=0 NormalX=0 NormalY=0 NormalZ=1 AngleXU=0 Radius=5.5
  constraints (2):
    c: Coincident(g0,g-3)
    c: Radius(g0) = 5.5
FEATURE [PartDesign::Pad] Pad877
  BaseFeature = -> Pad893
  Length = 0.5
  Length2 = 100
  Profile = -> Sketch2007
  Type = 0
FEATURE [Sketcher::SketchObject] Sketch2023
  ExternalGeometry = -> [Pad877]
  MapMode = 5
  Placement = pos=(0,0,39.1) rot=(0,0,1;0rad)
  Support = -> [Pad877]
  sketch-geometry (1):
    g0: Circle CenterX=0 CenterY=10.15 CenterZ=0 NormalX=0 NormalY=0 NormalZ=1 AngleXU=0 Radius=3
  constraints (2):
    c: Coincident(g0,g-3)
    c: Radius(g0) = 3
FEATURE [PartDesign::Pad] Pad882
  BaseFeature = -> Pad877
  Length = 4
  Length2 = 100
  Profile = -> Sketch2023
  Type = 0
FEATURE [Sketcher::SketchObject] Sketch2005
  ExternalGeometry = -> [Pad882]
  MapMode = 5
  Placement = pos=(0,0,43.1) rot=(0,0,1;0rad)
  Support = -> [Pad882]
  sketch-geometry (1):
    g0: Circle CenterX=0 CenterY=10.15 CenterZ=0 NormalX=0 NormalY=0 NormalZ=1 AngleXU=0 Radius=1.5
  constraints (2):
    c: Coincident(g0,g-3)
    c: Radius(g0) = 1.5
FEATURE [PartDesign::Pocket] Pocket738
  BaseFeature = -> Pad882
  Length = 5
  Length2 = 100
  Profile = -> Sketch2005
  Type = 0
FEATURE [Sketcher::SketchObject] Sketch2002
  MapMode = 5
  Placement = pos=(0,0,29.1) rot=(0,0,1;0rad)
  Support = -> [Pocket738]
  sketch-geometry (4):
    g0: Circle CenterX=-4.91157 CenterY=25.3 CenterZ=0 NormalX=0 NormalY=0 NormalZ=1 AngleXU=0 Radius=2.25
    g1: Circle CenterX=4.91157 CenterY=25.3 CenterZ=0 NormalX=0 NormalY=0 NormalZ=1 AngleXU=0 Radius=2.25
    g2: Circle CenterX=-4.91157 CenterY=-25.3 CenterZ=0 NormalX=0 NormalY=0 NormalZ=1 AngleXU=0 Radius=2.25
    g3: Circle CenterX=4.91157 CenterY=-25.3 CenterZ=0 NormalX=0 NormalY=0 NormalZ=1 AngleXU=0 Radius=2.25
  constraints (8):
    c: Equal(g3,g2)
    c: Equal(g2,g1)
    c: Equal(g1,g0)
    c: Radius(g1) = 2.25
    c: Symmetric(g1,g0,g-2)
    c: Symmetric(g3,g2,g-2)
    c: Symmetric(g3,g1,g-1)
    c: DistanceY(g3,g1) = 50.6
FEATURE [PartDesign::Pocket] Pocket737
  BaseFeature = -> Pocket738
  Length = 5
  Length2 = 100
  Profile = -> Sketch2002
  Type = 0
FEATURE [Sketcher::SketchObject] Sketch2016
  MapMode = 5
  Placement = pos=(0,0,29.1) rot=(0,0,1;0rad)
  Support = -> [Pocket737]
  sketch-geometry (8):
    g0: LineSegment StartX=-0.5 StartY=26.8 StartZ=0 EndX=0.5 EndY=26.8 EndZ=0
    g1: LineSegment StartX=0.5 StartY=26.8 StartZ=0 EndX=0.5 EndY=20.15 EndZ=0
    g2: LineSegment StartX=0.5 StartY=20.15 StartZ=0 EndX=-0.5 EndY=20.15 EndZ=0
    g3: LineSegment StartX=-0.5 StartY=20.15 StartZ=0 EndX=-0.5 EndY=26.8 EndZ=0
    g4: LineSegment StartX=-0.5 StartY=-20.15 StartZ=0 EndX=0.5 EndY=-20.15 EndZ=0
    g5: LineSegment StartX=0.5 StartY=-20.15 StartZ=0 EndX=0.5 EndY=-26.8 EndZ=0
    g6: LineSegment StartX=0.5 StartY=-26.8 StartZ=0 EndX=-0.5 EndY=-26.8 EndZ=0
    g7: LineSegment StartX=-0.5 StartY=-26.8 StartZ=0 EndX=-0.5 EndY=-20.15 EndZ=0
  constraints (20):
    c: Coincident(g0,g1)
    c: Coincident(g1,g2)
    c: Coincident(g2,g3)
    c: Coincident(g3,g0)
    c: Horizontal(g2)
    c: Vertical(g1)
    c: Vertical(g3)
    c: Coincident(g4,g5)
    c: Coincident(g5,g6)
    c: Coincident(g6,g7)
    c: Coincident(g7,g4)
    c: Horizontal(g6)
    c: Vertical(g7)
    c: Symmetric(g4,g4,g-2)
    c: Symmetric(g0,g0,g-2)
    c: Symmetric(g0,g5,g-1)
    c: DistanceY(g5,g0) = 53.6
    c: DistanceY(g4,g1) = 40.3
    c: DistanceX(g0,g0) = 1
    c: Symmetric(g4,g1,g-1)
FEATURE [PartDesign::Pad] Pad873
  BaseFeature = -> Pocket737
  Length = 2
  Length2 = 100
  Profile = -> Sketch2016
  Type = 0
FEATURE [Sketcher::SketchObject] Sketch2003
  ExternalGeometry = -> [Pad873]
  MapMode = 5
  Placement = pos=(0.5,0,0) rot=(0.57735,0.57735,0.57735;2.0944rad)
  Support = -> [Pad873]
  sketch-geometry (6):
    g0: LineSegment StartX=-26.8 StartY=29.1 StartZ=0 EndX=-26.8 EndY=31.1 EndZ=0
    g1: LineSegment StartX=-26.8 StartY=31.1 StartZ=0 EndX=-20.15 EndY=31.1 EndZ=0
    g2: LineSegment StartX=-20.15 StartY=31.1 StartZ=0 EndX=-26.8 EndY=29.1 EndZ=0
    g3: LineSegment StartX=20.15 StartY=31.1 StartZ=0 EndX=26.8 EndY=31.1 EndZ=0
    g4: LineSegment StartX=26.8 StartY=31.1 StartZ=0 EndX=26.8 EndY=29.1 EndZ=0
    g5: LineSegment StartX=26.8 StartY=29.1 StartZ=0 EndX=20.15 EndY=31.1 EndZ=0
  constraints (14):
    c: Vertical(g0)
    c: Coincident(g0,g1)
    c: Horizontal(g1)
    c: Coincident(g1,g2)
    c: Coincident(g2,g0)
    c: Coincident(g3,g4)
    c: Coincident(g4,g5)
    c: Coincident(g5,g3)
    c: Symmetric(g0,g4,g-2)
    c: Symmetric(g3,g0,g-2)
    c: Symmetric(g1,g3,g-2)
    c: DistanceX(g0,g3) = 53.6
    c: DistanceY(g4,g4) = 2
    c: Coincident(g3,g-3)
FEATURE [PartDesign::Pocket] Pocket736
  BaseFeature = -> Pad873
  Length = 1
  Length2 = 100
  Profile = -> Sketch2003
  Type = 0
FEATURE [PartDesign::Fillet] Fillet245
  Base = -> Pocket736 [Edge26,Edge27,Edge72,Edge63,Edge70,Edge78,Edge51,Edge49,Edge71,Edge50,Edge79,Edge86,Edge30,Edge21,Edge4,Edge29,Edge105,Edge107,Edge109,Edge111,Edge113,Edge114,Edge123]
  BaseFeature = -> Pocket736
  Radius = 0.4
FEATURE [Sketcher::SketchObject] Sketch2010
  MapMode = 5
  Placement = pos=(0,20.15,0) rot=(0,0.707107,0.707107;3.14159rad)
  Support = -> [Fillet245]
  sketch-geometry (4):
    g0: LineSegment StartX=-3.25 StartY=2 StartZ=0 EndX=3.25 EndY=2 EndZ=0
    g1: LineSegment StartX=3.25 StartY=2 StartZ=0 EndX=3.25 EndY=6 EndZ=0
    g2: LineSegment StartX=3.25 StartY=6 StartZ=0 EndX=-3.25 EndY=6 EndZ=0
    g3: LineSegment StartX=-3.25 StartY=6 StartZ=0 EndX=-3.25 EndY=2 EndZ=0
  constraints (11):
    c: Coincident(g0,g1)
    c: Coincident(g1,g2)
    c: Coincident(g2,g3)
    c: Coincident(g3,g0)
    c: Horizontal(g0)
    c: Vertical(g1)
    c: Vertical(g3)
    c: DistanceY(g-1,g0) = 2
    c: DistanceY(g1,g1) = 4
    c: Symmetric(g2,g1,g-2)
    c: DistanceX(g2,g2) = 6.5
FEATURE [PartDesign::Pad] Pad884
  BaseFeature = -> Fillet245
  Length = 1
  Length2 = 100
  Profile = -> Sketch2010
  Type = 0
FEATURE [Sketcher::SketchObject] Sketch2009
  MapMode = 5
  Placement = pos=(0,21.15,0) rot=(0,0.707107,0.707107;3.14159rad)
  Support = -> [Pad884]
  sketch-geometry (4):
    g0: LineSegment StartX=-2.75 StartY=5.5 StartZ=0 EndX=2.75 EndY=5.5 EndZ=0
    g1: LineSegment StartX=2.75 StartY=5.5 StartZ=0 EndX=2.75 EndY=2.5 EndZ=0
    g2: LineSegment StartX=2.75 StartY=2.5 StartZ=0 EndX=-2.75 EndY=2.5 EndZ=0
    g3: LineSegment StartX=-2.75 StartY=2.5 StartZ=0 EndX=-2.75 EndY=5.5 EndZ=0
  constraints (11):
    c: Coincident(g0,g1)
    c: Coincident(g1,g2)
    c: Coincident(g2,g3)
    c: Coincident(g3,g0)
    c: Horizontal(g0)
    c: Vertical(g1)
    c: Vertical(g3)
    c: Symmetric(g1,g2,g-2)
    c: DistanceY(g1,g0) = 3
    c: DistanceY(g-1,g1) = 2.5
    c: DistanceX(g0,g0) = 5.5
FEATURE [PartDesign::Pad] Pad872
  BaseFeature = -> Pad884
  Length = 4
  Length2 = 100
  Profile = -> Sketch2009
  Type = 0
FEATURE [Sketcher::SketchObject] Sketch2013
  MapMode = 5
  Placement = pos=(0,0,0) rot=(1,0,0;3.14159rad)
  Support = -> [Pad872]
  sketch-geometry (4):
    g0: LineSegment StartX=-10 StartY=-20.15 StartZ=0 EndX=10 EndY=-20.15 EndZ=0
    g1: LineSegment StartX=10 StartY=-20.15 StartZ=0 EndX=10 EndY=20.15 EndZ=0
    g2: LineSegment StartX=10 StartY=20.15 StartZ=0 EndX=-10 EndY=20.15 EndZ=0
    g3: LineSegment StartX=-10 StartY=20.15 StartZ=0 EndX=-10 EndY=-20.15 EndZ=0
  constraints (10):
    c: Coincident(g0,g1)
    c: Coincident(g1,g2)
    c: Coincident(g2,g3)
    c: Coincident(g3,g0)
    c: Horizontal(g0)
    c: Vertical(g1)
    c: Symmetric(g2,g1,g-2)
    c: Symmetric(g0,g2,g-1)
    c: DistanceX(g2,g2) = 20
    c: DistanceY(g1,g1) = 40.3
FEATURE [PartDesign::Pad] Pad894
  BaseFeature = -> Pad872
  Length = 2
  Length2 = 100
  Profile = -> Sketch2013
  Type = 0
FEATURE [PartDesign::Chamfer] Chamfer422
  Base = -> Pad894 [Face7]
  BaseFeature = -> Pad894
  Size = 1.5
FEATURE [PartDesign::Fillet] Fillet244
  Base = -> Chamfer422 [Edge1,Edge7,Edge18,Edge4,Face12]
  BaseFeature = -> Chamfer422
  Radius = 0.4
FEATURE [Sketcher::SketchObject] Sketch2004
  ExternalGeometry = -> [Fillet244]
  MapMode = 5
  Placement = pos=(0,0,43.1) rot=(0,0,1;0rad)
  Support = -> [Fillet244]
  sketch-geometry (1):
    g0: Circle CenterX=0 CenterY=10.15 CenterZ=0 NormalX=0 NormalY=0 NormalZ=1 AngleXU=0 Radius=3
  constraints (2):
    c: Coincident(g0,g-3)
    c: Radius(g0) = 3
FEATURE [PartDesign::Pocket] Pocket741
  BaseFeature = -> Fillet244
  Length = 5
  Length2 = 100
  Profile = -> Sketch2004
  Type = 0
FEATURE [PartDesign::Body] Body558  label="MG996R013"
  Group = -> [Sketch2017,Pad890,Sketch2008,Pad887,Sketch2006,Pad885,Sketch2011,Pad876,Sketch2019,Pad893,Sketch2007,Pad877,Sketch2023,Pad882,Sketch2005,Pocket738,Sketch2002,Pocket737,Sketch2016,Pad873,Sketch2003,Pocket736,Fillet245,Sketch2010,Pad884,Sketch2009,Pad872,Sketch2013,Pad894,Chamfer422,Fillet244,Sketch2004,Pocket741]
  Origin = -> Origin787
  Tip = -> Pocket741
FEATURE [App::Part] Part219  label="Servo013"
  Group = -> [Body558,Body561,Body560,Body557,Body559]
  Origin = -> Origin784
  Placement = pos=(-21.1341,-60.6,200.491) rot=(0.57735,0.57735,0.57735;2.0944rad)
FEATURE [PartDesign::Pad] Pad895  label="M3 Nut Primitive178"
  Length = 1.2
  Length2 = 1.2
  Profile = -> Sketch2022
  Type = 4
FEATURE [Sketcher::SketchObject] Sketch2021
  ExternalGeometry = -> [Pad895]
  MapMode = 5
  Placement = pos=(0,0,0) rot=(0.57735,0.57735,0.57735;2.0944rad)
  Support = -> [YZ_Plane773]
  sketch-geometry (6):
    g0: LineSegment StartX=-2.67543 StartY=1.2 StartZ=0 EndX=-3.67543 EndY=1.2 EndZ=0
    g1: LineSegment StartX=-3.67543 StartY=1.2 StartZ=0 EndX=-3.67543 EndY=-1.2 EndZ=0
    g2: LineSegment StartX=-3.67543 StartY=-1.2 StartZ=0 EndX=-2.67543 EndY=-1.2 EndZ=0
    g3: LineSegment StartX=-2.67543 StartY=-1.2 StartZ=0 EndX=-3.17543 EndY=-1 EndZ=0
    g4: LineSegment StartX=-3.17543 StartY=-1 StartZ=0 EndX=-3.17543 EndY=1 EndZ=0
    g5: LineSegment StartX=-3.17543 StartY=1 StartZ=0 EndX=-2.67543 EndY=1.2 EndZ=0
  constraints (15):
    c: Horizontal(g0)
    c: Coincident(g0,g1)
    c: Coincident(g1,g2)
    c: Coincident(g2,g3)
    c: Coincident(g3,g4)
    c: Coincident(g4,g5)
    c: Coincident(g5,g0)
    c: Symmetric(g4,g3,g-1)
    c: Symmetric(g0,g2,g-1)
    c: Symmetric(g1,g0,g-1)
    c: DistanceX(g0,g4) = 0.5
    c: DistanceY(g3,g4) = 2
    c: DistanceY(g1,g0) = 2.4
    c: PointOnObject(g3,g-3)
    c: DistanceX(g4,g0) = 0.5
FEATURE [PartDesign::Groove] Groove186  label="M3 Nut Smooth178"
  Angle = 360
  Axis = (-2e-16,3e-16,1)
  Base = (0,0,0)
  BaseFeature = -> Pad895
  Profile = -> Sketch2021
  ReferenceAxis = -> Sketch2021 [V_Axis]
  Reversed = true
FEATURE [PartDesign::Chamfer] Chamfer416  label="M3 Nut Smooth Hole177"
  Base = -> Groove186 [Edge24,Edge23]
  BaseFeature = -> Groove186
  Size = 0.2
FEATURE [PartDesign::Body] Body555  label="M3 Nut099"
  Group = -> [Sketch2022,Pad895,Sketch2021,Groove186,Chamfer416]
  Origin = -> Origin793
  Placement = pos=(5e-14,-55.6,224.85) rot=(0.57735,-0.57735,0.57735;4.18879rad)
  Tip = -> Chamfer416
FEATURE [PartDesign::Pad] Pad896  label="M3x20 Head074"
  Length = 3
  Length2 = 100
  Profile = -> Sketch2038
  Type = 0
FEATURE [Sketcher::SketchObject] Sketch2027
  MapMode = 5
  Placement = pos=(0,0,3) rot=(0,0,1;0rad)
  Support = -> [Pad896]
  sketch-geometry (1):
    g0: Circle CenterX=0 CenterY=0 CenterZ=0 NormalX=0 NormalY=0 NormalZ=1 AngleXU=0 Radius=1.5
  constraints (2):
    c: Coincident(g0,g-1)
    c: Radius(g0) = 1.5
FEATURE [PartDesign::Pad] Pad880  label="M3x20 Thread072"
  BaseFeature = -> Pad896
  Length = 20
  Length2 = 100
  Profile = -> Sketch2027
  Type = 0
FEATURE [Sketcher::SketchObject] Sketch2037
  MapMode = 5
  Placement = pos=(0,0,0) rot=(1,0,0;3.14159rad)
  Support = -> [Pad880]
  sketch-geometry (7):
    g0: LineSegment StartX=1.275 StartY=0.736122 StartZ=0 EndX=0 EndY=1.47224 EndZ=0
    g1: LineSegment StartX=0 StartY=1.47224 StartZ=0 EndX=-1.275 EndY=0.736122 EndZ=0
    g2: LineSegment StartX=-1.275 StartY=0.736122 StartZ=0 EndX=-1.275 EndY=-0.736122 EndZ=0
    g3: LineSegment StartX=-1.275 StartY=-0.736122 StartZ=0 EndX=1.34766e-11 EndY=-1.47224 EndZ=0
    g4: LineSegment StartX=1.34766e-11 StartY=-1.47224 StartZ=0 EndX=1.275 EndY=-0.736122 EndZ=0
    g5: LineSegment StartX=1.275 StartY=-0.736122 StartZ=0 EndX=1.275 EndY=0.736122 EndZ=0
    g6: Circle [constr] CenterX=0 CenterY=0 CenterZ=0 NormalX=0 NormalY=0 NormalZ=1 AngleXU=0 Radius=1.47224
  constraints (16):
    c: Coincident(g0,g1)
    c: Coincident(g1,g2)
    c: Coincident(g2,g3)
    c: Coincident(g3,g4)
    c: Coincident(g4,g5)
    c: Coincident(g5,g0)
    c: Equal(g0, g1-g5) x5
    c: PointOnObject(g0,g6)
    c: PointOnObject(g1,g6)
    c: PointOnObject(g2,g6)
    c: PointOnObject(g3,g6)
    c: PointOnObject(g4,g6)
    c: PointOnObject(g5,g6)
    c: Coincident(g6,g-1)
    c: PointOnObject(g0,g-2)
    c: DistanceX(g1,g0) = 2.55
FEATURE [PartDesign::Pocket] Pocket744  label="M3x20 Wrench074"
  BaseFeature = -> Pad880
  Length = 1.3
  Length2 = 100
  Profile = -> Sketch2037
  Type = 0
FEATURE [PartDesign::Chamfer] Chamfer423  label="M3x20 Smooth073"
  Base = -> Pocket744 [Face11,Edge2,Edge24,Edge3]
  BaseFeature = -> Pocket744
  Size = 0.2
FEATURE [PartDesign::Body] Body564  label="M3x118"
  Group = -> [Sketch2038,Pad896,Sketch2027,Pad880,Sketch2037,Pocket744,Chamfer423]
  Origin = -> Origin786
  Placement = pos=(11.3,-65.6,176.35) rot=(0,-1,0;1.5708rad)
  Tip = -> Chamfer423
FEATURE [PartDesign::Pad] Pad898  label="M3x20 Head075"
  Length = 3
  Length2 = 100
  Profile = -> Sketch2040
  Type = 0
FEATURE [Sketcher::SketchObject] Sketch2041
  MapMode = 5
  Placement = pos=(0,0,3) rot=(0,0,1;0rad)
  Support = -> [Pad898]
  sketch-geometry (1):
    g0: Circle CenterX=0 CenterY=0 CenterZ=0 NormalX=0 NormalY=0 NormalZ=1 AngleXU=0 Radius=1.5
  constraints (2):
    c: Coincident(g0,g-1)
    c: Radius(g0) = 1.5
FEATURE [PartDesign::Pad] Pad897  label="M3x20 Thread074"
  BaseFeature = -> Pad898
  Length = 20
  Length2 = 100
  Profile = -> Sketch2041
  Type = 0
FEATURE [Sketcher::SketchObject] Sketch2039
  MapMode = 5
  Placement = pos=(0,0,0) rot=(1,0,0;3.14159rad)
  Support = -> [Pad897]
  sketch-geometry (7):
    g0: LineSegment StartX=1.275 StartY=0.736122 StartZ=0 EndX=0 EndY=1.47224 EndZ=0
    g1: LineSegment StartX=0 StartY=1.47224 StartZ=0 EndX=-1.275 EndY=0.736122 EndZ=0
    g2: LineSegment StartX=-1.275 StartY=0.736122 StartZ=0 EndX=-1.275 EndY=-0.736122 EndZ=0
    g3: LineSegment StartX=-1.275 StartY=-0.736122 StartZ=0 EndX=1.34766e-11 EndY=-1.47224 EndZ=0
    g4: LineSegment StartX=1.34766e-11 StartY=-1.47224 StartZ=0 EndX=1.275 EndY=-0.736122 EndZ=0
    g5: LineSegment StartX=1.275 StartY=-0.736122 StartZ=0 EndX=1.275 EndY=0.736122 EndZ=0
    g6: Circle [constr] CenterX=0 CenterY=0 CenterZ=0 NormalX=0 NormalY=0 NormalZ=1 AngleXU=0 Radius=1.47224
  constraints (16):
    c: Coincident(g0,g1)
    c: Coincident(g1,g2)
    c: Coincident(g2,g3)
    c: Coincident(g3,g4)
    c: Coincident(g4,g5)
    c: Coincident(g5,g0)
    c: Equal(g0, g1-g5) x5
    c: PointOnObject(g0,g6)
    c: PointOnObject(g1,g6)
    c: PointOnObject(g2,g6)
    c: PointOnObject(g3,g6)
    c: PointOnObject(g4,g6)
    c: PointOnObject(g5,g6)
    c: Coincident(g6,g-1)
    c: PointOnObject(g0,g-2)
    c: DistanceX(g1,g0) = 2.55
FEATURE [PartDesign::Pocket] Pocket740  label="M3x20 Wrench071"
  BaseFeature = -> Pad897
  Length = 1.3
  Length2 = 100
  Profile = -> Sketch2039
  Type = 0
FEATURE [PartDesign::Chamfer] Chamfer421  label="M3x20 Smooth072"
  Base = -> Pocket740 [Face11,Edge2,Edge24,Edge3]
  BaseFeature = -> Pocket740
  Size = 0.2
FEATURE [PartDesign::Body] Body567  label="M3x120"
  Group = -> [Sketch2040,Pad898,Sketch2041,Pad897,Sketch2039,Pocket740,Chamfer421]
  Origin = -> Origin789
  Placement = pos=(11.3,-55.6,176.35) rot=(0,-1,0;1.5708rad)
  Tip = -> Chamfer421
FEATURE [App::Part] Part221  label="Servo Scres003"
  Group = -> [Body562,Body565,Body564,Body567]
  Origin = -> Origin790
FEATURE [Sketcher::SketchObject] Sketch2042
  MapMode = 5
  Placement = pos=(0,0,0) rot=(1,0,0;1.5708rad)
  Support = -> [XZ_Plane791]
  sketch-geometry (8):
    g0: LineSegment StartX=-1.5 StartY=2.25 StartZ=0 EndX=-3.25 EndY=2.25 EndZ=0
    g1: LineSegment StartX=-3.25 StartY=2.25 StartZ=0 EndX=-3.25 EndY=1.25 EndZ=0
    g2: LineSegment StartX=-3.25 StartY=1.25 StartZ=0 EndX=-2 EndY=1.25 EndZ=0
    g3: LineSegment StartX=-2 StartY=1.25 StartZ=0 EndX=-2 EndY=-1.25 EndZ=0
    g4: LineSegment StartX=-2 StartY=-1.25 StartZ=0 EndX=-3.25 EndY=-1.25 EndZ=0
    g5: LineSegment StartX=-3.25 StartY=-1.25 StartZ=0 EndX=-3.25 EndY=-2.25 EndZ=0
    g6: LineSegment StartX=-3.25 StartY=-2.25 StartZ=0 EndX=-1.5 EndY=-2.25 EndZ=0
    g7: LineSegment StartX=-1.5 StartY=-2.25 StartZ=0 EndX=-1.5 EndY=2.25 EndZ=0
  constraints (23):
    c: Horizontal(g0)
    c: Coincident(g0,g1)
    c: Vertical(g1)
    c: Coincident(g1,g2)
    c: Horizontal(g2)
    c: Coincident(g2,g3)
    c: Vertical(g3)
    c: Coincident(g3,g4)
    c: Horizontal(g4)
    c: Coincident(g4,g5)
    c: Vertical(g5)
    c: Coincident(g5,g6)
    c: Horizontal(g6)
    c: Coincident(g6,g7)
    c: Vertical(g7)
    c: Coincident(g0,g7)
    c: Equal(g1,g5)
    c: Symmetric(g4,g1,g-1)
    c: DistanceX(g0,g-1) = 1.5
    c: DistanceY(g3,g3) = 2.5
    c: DistanceY(g7,g7) = 4.5
    c: DistanceX(g0,g-1) = 3.25
    c: DistanceX(g2,g-1) = 2
FEATURE [Sketcher::SketchObject] Sketch2043
  MapMode = 5
  Placement = pos=(0,0,0) rot=(1,0,0;1.5708rad)
  Support = -> [XZ_Plane793]
  sketch-geometry (8):
    g0: LineSegment StartX=-1.5 StartY=2.25 StartZ=0 EndX=-3.25 EndY=2.25 EndZ=0
    g1: LineSegment StartX=-3.25 StartY=2.25 StartZ=0 EndX=-3.25 EndY=1.25 EndZ=0
    g2: LineSegment StartX=-3.25 StartY=1.25 StartZ=0 EndX=-2 EndY=1.25 EndZ=0
    g3: LineSegment StartX=-2 StartY=1.25 StartZ=0 EndX=-2 EndY=-1.25 EndZ=0
    g4: LineSegment StartX=-2 StartY=-1.25 StartZ=0 EndX=-3.25 EndY=-1.25 EndZ=0
    g5: LineSegment StartX=-3.25 StartY=-1.25 StartZ=0 EndX=-3.25 EndY=-2.25 EndZ=0
    g6: LineSegment StartX=-3.25 StartY=-2.25 StartZ=0 EndX=-1.5 EndY=-2.25 EndZ=0
    g7: LineSegment StartX=-1.5 StartY=-2.25 StartZ=0 EndX=-1.5 EndY=2.25 EndZ=0
  constraints (23):
    c: Horizontal(g0)
    c: Coincident(g0,g1)
    c: Vertical(g1)
    c: Coincident(g1,g2)
    c: Horizontal(g2)
    c: Coincident(g2,g3)
    c: Vertical(g3)
    c: Coincident(g3,g4)
    c: Horizontal(g4)
    c: Coincident(g4,g5)
    c: Vertical(g5)
    c: Coincident(g5,g6)
    c: Horizontal(g6)
    c: Coincident(g6,g7)
    c: Vertical(g7)
    c: Coincident(g0,g7)
    c: Equal(g1,g5)
    c: Symmetric(g4,g1,g-1)
    c: DistanceX(g0,g-1) = 1.5
    c: DistanceY(g3,g3) = 2.5
    c: DistanceY(g7,g7) = 4.5
    c: DistanceX(g0,g-1) = 3.25
    c: DistanceX(g2,g-1) = 2
FEATURE [Sketcher::SketchObject] Sketch2044
  MapMode = 5
  Placement = pos=(0,0,0) rot=(1,0,0;1.5708rad)
  Support = -> [XZ_Plane794]
  sketch-geometry (8):
    g0: LineSegment StartX=-1.5 StartY=2.25 StartZ=0 EndX=-3.25 EndY=2.25 EndZ=0
    g1: LineSegment StartX=-3.25 StartY=2.25 StartZ=0 EndX=-3.25 EndY=1.25 EndZ=0
    g2: LineSegment StartX=-3.25 StartY=1.25 StartZ=0 EndX=-2 EndY=1.25 EndZ=0
    g3: LineSegment StartX=-2 StartY=1.25 StartZ=0 EndX=-2 EndY=-1.25 EndZ=0
    g4: LineSegment StartX=-2 StartY=-1.25 StartZ=0 EndX=-3.25 EndY=-1.25 EndZ=0
    g5: LineSegment StartX=-3.25 StartY=-1.25 StartZ=0 EndX=-3.25 EndY=-2.25 EndZ=0
    g6: LineSegment StartX=-3.25 StartY=-2.25 StartZ=0 EndX=-1.5 EndY=-2.25 EndZ=0
    g7: LineSegment StartX=-1.5 StartY=-2.25 StartZ=0 EndX=-1.5 EndY=2.25 EndZ=0
  constraints (23):
    c: Horizontal(g0)
    c: Coincident(g0,g1)
    c: Vertical(g1)
    c: Coincident(g1,g2)
    c: Horizontal(g2)
    c: Coincident(g2,g3)
    c: Vertical(g3)
    c: Coincident(g3,g4)
    c: Horizontal(g4)
    c: Coincident(g4,g5)
    c: Vertical(g5)
    c: Coincident(g5,g6)
    c: Horizontal(g6)
    c: Coincident(g6,g7)
    c: Vertical(g7)
    c: Coincident(g0,g7)
    c: Equal(g1,g5)
    c: Symmetric(g4,g1,g-1)
    c: DistanceX(g0,g-1) = 1.5
    c: DistanceY(g3,g3) = 2.5
    c: DistanceY(g7,g7) = 4.5
    c: DistanceX(g0,g-1) = 3.25
    c: DistanceX(g2,g-1) = 2
FEATURE [Sketcher::SketchObject] Sketch2045
  MapMode = 5
  Placement = pos=(0,0,0) rot=(1,0,0;1.5708rad)
  Support = -> [XZ_Plane792]
  sketch-geometry (8):
    g0: LineSegment StartX=-1.5 StartY=2.25 StartZ=0 EndX=-3.25 EndY=2.25 EndZ=0
    g1: LineSegment StartX=-3.25 StartY=2.25 StartZ=0 EndX=-3.25 EndY=1.25 EndZ=0
    g2: LineSegment StartX=-3.25 StartY=1.25 StartZ=0 EndX=-2 EndY=1.25 EndZ=0
    g3: LineSegment StartX=-2 StartY=1.25 StartZ=0 EndX=-2 EndY=-1.25 EndZ=0
    g4: LineSegment StartX=-2 StartY=-1.25 StartZ=0 EndX=-3.25 EndY=-1.25 EndZ=0
    g5: LineSegment StartX=-3.25 StartY=-1.25 StartZ=0 EndX=-3.25 EndY=-2.25 EndZ=0
    g6: LineSegment StartX=-3.25 StartY=-2.25 StartZ=0 EndX=-1.5 EndY=-2.25 EndZ=0
    g7: LineSegment StartX=-1.5 StartY=-2.25 StartZ=0 EndX=-1.5 EndY=2.25 EndZ=0
  constraints (23):
    c: Horizontal(g0)
    c: Coincident(g0,g1)
    c: Vertical(g1)
    c: Coincident(g1,g2)
    c: Horizontal(g2)
    c: Coincident(g2,g3)
    c: Vertical(g3)
    c: Coincident(g3,g4)
    c: Horizontal(g4)
    c: Coincident(g4,g5)
    c: Vertical(g5)
    c: Coincident(g5,g6)
    c: Horizontal(g6)
    c: Coincident(g6,g7)
    c: Vertical(g7)
    c: Coincident(g0,g7)
    c: Equal(g1,g5)
    c: Symmetric(g4,g1,g-1)
    c: DistanceX(g0,g-1) = 1.5
    c: DistanceY(g3,g3) = 2.5
    c: DistanceY(g7,g7) = 4.5
    c: DistanceX(g0,g-1) = 3.25
    c: DistanceX(g2,g-1) = 2
FEATURE [PartDesign::Revolution] Revolution048
  Angle = 360
  Axis = (0,2e-16,1)
  Base = (0,0,0)
  Placement = pos=(0,0,0) rot=(1,0,0;1.5708rad)
  Profile = -> Sketch2045
  ReferenceAxis = -> Sketch2045 [V_Axis]
FEATURE [PartDesign::Fillet] Fillet249
  Base = -> Revolution048 [Face2,Face6,Edge1,Edge11,Face4]
  BaseFeature = -> Revolution048
  Placement = pos=(0,0,0) rot=(1,0,0;1.5708rad)
  Radius = 0.25
FEATURE [PartDesign::Body] Body569  label="Rubber Dampener047"
  Group = -> [Sketch2045,Revolution048,Fillet249]
  Origin = -> Origin798
  Placement = pos=(-96.5,-12.25,127.7) rot=(-1,0,0;1.5708rad)
  Tip = -> Fillet249
FEATURE [PartDesign::Revolution] Revolution049
  Angle = 360
  Axis = (0,2e-16,1)
  Base = (0,0,0)
  Placement = pos=(0,0,0) rot=(1,0,0;1.5708rad)
  Profile = -> Sketch2044
  ReferenceAxis = -> Sketch2044 [V_Axis]
FEATURE [PartDesign::Fillet] Fillet247
  Base = -> Revolution049 [Face2,Face6,Edge1,Edge11,Face4]
  BaseFeature = -> Revolution049
  Placement = pos=(0,0,0) rot=(1,0,0;1.5708rad)
  Radius = 0.25
FEATURE [PartDesign::Body] Body568  label="Rubber Dampener046"
  Group = -> [Sketch2044,Revolution049,Fillet247]
  Origin = -> Origin795
  Placement = pos=(-55.25,-12.25,100.75) rot=(-1,0,0;1.5708rad)
  Tip = -> Fillet247
FEATURE [PartDesign::Revolution] Revolution050
  Angle = 360
  Axis = (0,2e-16,1)
  Base = (0,0,0)
  Placement = pos=(0,0,0) rot=(1,0,0;1.5708rad)
  Profile = -> Sketch2042
  ReferenceAxis = -> Sketch2042 [V_Axis]
FEATURE [PartDesign::Fillet] Fillet248
  Base = -> Revolution050 [Face2,Face6,Edge1,Edge11,Face4]
  BaseFeature = -> Revolution050
  Placement = pos=(0,0,0) rot=(1,0,0;1.5708rad)
  Radius = 0.25
FEATURE [PartDesign::Body] Body570  label="Rubber Dampener048"
  Group = -> [Sketch2042,Revolution050,Fillet248]
  Origin = -> Origin796
  Placement = pos=(-89.5,-12.25,134.7) rot=(-1,0,0;1.5708rad)
  Tip = -> Fillet248
FEATURE [PartDesign::Revolution] Revolution051
  Angle = 360
  Axis = (0,2e-16,1)
  Base = (0,0,0)
  Placement = pos=(0,0,0) rot=(1,0,0;1.5708rad)
  Profile = -> Sketch2043
  ReferenceAxis = -> Sketch2043 [V_Axis]
FEATURE [PartDesign::Fillet] Fillet246
  Base = -> Revolution051 [Face2,Face6,Edge1,Edge11,Face4]
  BaseFeature = -> Revolution051
  Placement = pos=(0,0,0) rot=(1,0,0;1.5708rad)
  Radius = 0.25
FEATURE [PartDesign::Body] Body571  label="Rubber Dampener049"
  Group = -> [Sketch2043,Revolution051,Fillet246]
  Origin = -> Origin797
  Placement = pos=(-62.3,-12.25,93.7) rot=(-1,0,0;1.5708rad)
  Tip = -> Fillet246
FEATURE [App::Part] Part222  label="Rubber Dampeners012"
  Group = -> [Body570,Body569,Body568,Body571]
  Origin = -> Origin794
  Placement = pos=(18.7923,-33.3866,66.0791) rot=(0.357407,0.357407,-0.862856;1.71777rad)
FEATURE [App::Part] Part220  label="FL Shoulder Joint Servo003"
  Group = -> [Part219,Body556,Body566,Body563,Body555,Part221,Part222]
  Origin = -> Origin781
  Placement = pos=(-10.5,1.3e-15,0) rot=(0,0,1;3.14159rad)
FEATURE [App::Part] Part173  label="RR LEG"
  Group = -> [Part199,Part189,Part213,Part220]
  Origin = -> Origin643
  Placement = pos=(-205.85,-199.3,0) rot=(0,0,1;0rad)
FEATURE [Sketcher::SketchObject] Sketch
  MapMode = 5
  Support = -> [XY_Plane797]
  sketch-geometry (8):
    g0: LineSegment StartX=-35 StartY=70 StartZ=0 EndX=35 EndY=70 EndZ=0
    g1: LineSegment StartX=55 StartY=50 StartZ=0 EndX=55 EndY=25 EndZ=0
    g2: LineSegment StartX=30 StartY=0 StartZ=0 EndX=-30 EndY=0 EndZ=0
    g3: LineSegment StartX=-55 StartY=25 StartZ=0 EndX=-55 EndY=50 EndZ=0
    g4: ArcOfCircle CenterX=-35 CenterY=50 CenterZ=0 NormalX=0 NormalY=0 NormalZ=1 AngleXU=0 Radius=20 StartAngle=1.5708 EndAngle=3.14159
    g5: ArcOfCircle CenterX=35 CenterY=50 CenterZ=0 NormalX=0 NormalY=0 NormalZ=1 AngleXU=0 Radius=20 StartAngle=0 EndAngle=1.5708
    g6: ArcOfCircle CenterX=30 CenterY=25 CenterZ=0 NormalX=0 NormalY=0 NormalZ=1 AngleXU=0 Radius=25 StartAngle=4.71239 EndAngle=6.28319
    g7: ArcOfCircle CenterX=-30 CenterY=25 CenterZ=0 NormalX=0 NormalY=0 NormalZ=1 AngleXU=0 Radius=25 StartAngle=3.14159 EndAngle=4.71239
  constraints (19):
    c: Horizontal(g0)
    c: Horizontal(g2)
    c: Vertical(g1)
    c: Vertical(g3)
    c: Tangent(g3,g4) = 1.5708
    c: Tangent(g0,g4) = 1.5708
    c: Tangent(g0,g5) = 1.5708
    c: Tangent(g1,g5) = 1.5708
    c: Tangent(g1,g6) = 1.5708
    c: Tangent(g2,g6) = 1.5708
    c: Tangent(g2,g7) = 1.5708
    c: Tangent(g3,g7) = 1.5708
    c: Equal(g4,g5)
    c: Equal(g7,g6)
    c: Symmetric(g2,g2,g-1)
    c: Radius(g4) = 20
    c: Radius(g7) = 25
    c: DistanceY(g2,g0) = 70
    c: DistanceX(g3,g1) = 110
FEATURE [PartDesign::Pad] Pad  label="Baseplate"
  Length = 5
  Length2 = 100
  Profile = -> Sketch
  Type = 0
FEATURE [Sketcher::SketchObject] Sketch001
  MapMode = 5
  Placement = pos=(0,0,5) rot=(0,0,1;0rad)
  Support = -> [Pad]
  sketch-geometry (8):
    g0: LineSegment StartX=-10 StartY=58 StartZ=0 EndX=10 EndY=58 EndZ=0
    g1: LineSegment StartX=20 StartY=48 StartZ=0 EndX=20 EndY=22 EndZ=0
    g2: LineSegment StartX=10 StartY=12 StartZ=0 EndX=-10 EndY=12 EndZ=0
    g3: LineSegment StartX=-20 StartY=22 StartZ=0 EndX=-20 EndY=48 EndZ=0
    g4: ArcOfCircle CenterX=-10 CenterY=48 CenterZ=0 NormalX=0 NormalY=0 NormalZ=1 AngleXU=0 Radius=10 StartAngle=1.5708 EndAngle=3.14159
    g5: ArcOfCircle CenterX=10 CenterY=48 CenterZ=0 NormalX=0 NormalY=0 NormalZ=1 AngleXU=0 Radius=10 StartAngle=2e-16 EndAngle=1.5708
    g6: ArcOfCircle CenterX=10 CenterY=22 CenterZ=0 NormalX=0 NormalY=0 NormalZ=1 AngleXU=0 Radius=10 StartAngle=4.71239 EndAngle=6.28319
    g7: ArcOfCircle CenterX=-10 CenterY=22 CenterZ=0 NormalX=0 NormalY=0 NormalZ=1 AngleXU=0 Radius=10 StartAngle=3.14159 EndAngle=4.71239
  constraints (19):
    c: Horizontal(g0)
    c: Vertical(g1)
    c: Vertical(g3)
    c: Tangent(g3,g4) = 1.5708
    c: Tangent(g0,g4) = 1.5708
    c: Tangent(g0,g5) = 1.5708
    c: Tangent(g1,g5) = 1.5708
    c: Tangent(g1,g6) = 1.5708
    c: Tangent(g2,g6) = 1.5708
    c: Tangent(g2,g7) = 1.5708
    c: Tangent(g3,g7) = 1.5708
    c: Equal(g5,g4)
    c: Equal(g4,g7)
    c: Equal(g7,g6)
    c: Symmetric(g2,g2,g-2)
    c: DistanceX(g3,g1) = 40
    c: DistanceY(g-1,g2) = 12
    c: DistanceY(g2,g0) = 46
    c: Radius(g5) = 10
FEATURE [PartDesign::Pocket] Pocket  label="Accesshole004"
  BaseFeature = -> Pad
  Length = 5
  Length2 = 100
  Profile = -> Sketch001
  Type = 0
FEATURE [Sketcher::SketchObject] Sketch2046
  MapMode = 5
  Placement = pos=(0,0,5) rot=(0,0,1;0rad)
  Support = -> [Pocket]
  sketch-geometry (4):
    g0: Circle CenterX=-5 CenterY=6 CenterZ=0 NormalX=0 NormalY=0 NormalZ=1 AngleXU=0 Radius=1.6
    g1: Circle CenterX=5 CenterY=6 CenterZ=0 NormalX=0 NormalY=0 NormalZ=1 AngleXU=0 Radius=1.6
    g2: Circle CenterX=15 CenterY=64 CenterZ=0 NormalX=0 NormalY=0 NormalZ=1 AngleXU=0 Radius=1.6
    g3: Circle CenterX=-15 CenterY=64 CenterZ=0 NormalX=0 NormalY=0 NormalZ=1 AngleXU=0 Radius=1.6
  constraints (10):
    c: Symmetric(g0,g1,g-2)
    c: Symmetric(g3,g2,g-2)
    c: DistanceX(g3,g2) = 30
    c: DistanceX(g0,g1) = 10
    c: DistanceY(g-1,g0) = 6
    c: DistanceY(g-1,g2) = 64
    c: Radius(g1) = 1.6
    c: Equal(g2,g3)
    c: Equal(g3,g0)
    c: Equal(g0,g1)
FEATURE [PartDesign::Pocket] Pocket001  label="Screwholes008"
  BaseFeature = -> Pocket
  Length = 5
  Length2 = 100
  Profile = -> Sketch2046
  Type = 0
FEATURE [Sketcher::SketchObject] Sketch2048
  ExternalGeometry = -> [Pocket001]
  MapMode = 5
  Placement = pos=(0,0,5) rot=(0,0,1;0rad)
  Support = -> [Pocket001]
  sketch-geometry (4):
    g0: Circle CenterX=-15 CenterY=64 CenterZ=0 NormalX=0 NormalY=0 NormalZ=1 AngleXU=0 Radius=3
    g1: Circle CenterX=15 CenterY=64 CenterZ=0 NormalX=0 NormalY=0 NormalZ=1 AngleXU=0 Radius=3
    g2: Circle CenterX=-5 CenterY=6 CenterZ=0 NormalX=0 NormalY=0 NormalZ=1 AngleXU=0 Radius=3
    g3: Circle CenterX=5 CenterY=6 CenterZ=0 NormalX=0 NormalY=0 NormalZ=1 AngleXU=0 Radius=3
  constraints (8):
    c: Coincident(g0,g-3)
    c: Coincident(g1,g-4)
    c: Coincident(g2,g-5)
    c: Coincident(g3,g-6)
    c: Equal(g3,g2)
    c: Equal(g2,g0)
    c: Equal(g0,g1)
    c: Radius(g1) = 3
FEATURE [PartDesign::Pocket] Pocket002  label="Screwheads"
  BaseFeature = -> Pocket001
  Length = 3
  Length2 = 100
  Profile = -> Sketch2048
  Type = 0
FEATURE [Sketcher::SketchObject] Sketch2047
  MapMode = 5
  Placement = pos=(0,0,5) rot=(0,0,1;0rad)
  Support = -> [Pocket002]
  sketch-geometry (2):
    g0: Circle CenterX=-39 CenterY=44 CenterZ=0 NormalX=0 NormalY=0 NormalZ=1 AngleXU=0 Radius=6.15
    g1: Circle CenterX=39 CenterY=44 CenterZ=0 NormalX=0 NormalY=0 NormalZ=1 AngleXU=0 Radius=6.15
  constraints (5):
    c: Equal(g1,g0)
    c: Symmetric(g0,g1,g-2)
    c: DistanceX(g0,g1) = 78
    c: DistanceY(g-1,g0) = 44
    c: Radius(g0) = 6.15
FEATURE [PartDesign::Pocket] Pocket003  label="Servohorn Axis"
  BaseFeature = -> Pocket002
  Length = 5
  Length2 = 100
  Profile = -> Sketch2047
  Type = 0
FEATURE [Sketcher::SketchObject] Sketch2049
  ExternalGeometry = -> [Pocket003]
  MapMode = 5
  Placement = pos=(0,0,5) rot=(0,0,1;0rad)
  Support = -> [Pocket003]
  sketch-geometry (64):
    g0: LineSegment [constr] StartX=-39 StartY=57.5 StartZ=0 EndX=-50.6913 EndY=50.75 EndZ=0
    g1: LineSegment [constr] StartX=-50.6913 StartY=50.75 StartZ=0 EndX=-50.6913 EndY=37.25 EndZ=0
    g2: LineSegment [constr] StartX=-50.6913 StartY=37.25 StartZ=0 EndX=-39 EndY=30.5 EndZ=0
    g3: LineSegment [constr] StartX=-39 StartY=30.5 StartZ=0 EndX=-27.3087 EndY=37.25 EndZ=0
    g4: LineSegment [constr] StartX=-27.3087 StartY=37.25 StartZ=0 EndX=-27.3087 EndY=50.75 EndZ=0
    g5: LineSegment [constr] StartX=-27.3087 StartY=50.75 StartZ=0 EndX=-39 EndY=57.5 EndZ=0
    g6: Circle [constr] CenterX=-39 CenterY=44 CenterZ=0 NormalX=0 NormalY=0 NormalZ=1 AngleXU=0 Radius=13.5
    g7: LineSegment [constr] StartX=39 StartY=57.5 StartZ=0 EndX=27.3087 EndY=50.75 EndZ=0
    g8: LineSegment [constr] StartX=27.3087 StartY=50.75 StartZ=0 EndX=27.3087 EndY=37.25 EndZ=0
    g9: LineSegment [constr] StartX=27.3087 StartY=37.25 StartZ=0 EndX=39 EndY=30.5 EndZ=0
    g10: LineSegment [constr] StartX=39 StartY=30.5 StartZ=0 EndX=50.6913 EndY=37.25 EndZ=0
    g11: LineSegment [constr] StartX=50.6913 StartY=37.25 StartZ=0 EndX=50.6913 EndY=50.75 EndZ=0
    g12: LineSegment [constr] StartX=50.6913 StartY=50.75 StartZ=0 EndX=39 EndY=57.5 EndZ=0
    g13: Circle [constr] CenterX=39 CenterY=44 CenterZ=0 NormalX=0 NormalY=0 NormalZ=1 AngleXU=0 Radius=13.5
    g14: ArcOfCircle CenterX=-39 CenterY=57.5 CenterZ=0 NormalX=0 NormalY=0 NormalZ=1 AngleXU=0 Radius=2.6 StartAngle=0.15815 EndAngle=2.98344
    g15: ArcOfCircle CenterX=-27.3087 CenterY=50.75 CenterZ=0 NormalX=0 NormalY=0 NormalZ=1 AngleXU=0 Radius=2.6 StartAngle=5.39414 EndAngle=8.21943
    g16: ArcOfCircle CenterX=-27.3087 CenterY=37.25 CenterZ=0 NormalX=0 NormalY=0 NormalZ=1 AngleXU=0 Radius=2.6 StartAngle=4.34694 EndAngle=7.17223
    g17: ArcOfCircle CenterX=-39 CenterY=30.5 CenterZ=0 NormalX=0 NormalY=0 NormalZ=1 AngleXU=0 Radius=2.6 StartAngle=3.29974 EndAngle=6.12503
    g18: ArcOfCircle CenterX=-50.6913 CenterY=37.25 CenterZ=0 NormalX=0 NormalY=0 NormalZ=1 AngleXU=0 Radius=2.6 StartAngle=2.25255 EndAngle=5.07784
    g19: ArcOfCircle CenterX=-50.6913 CenterY=50.75 CenterZ=0 NormalX=0 NormalY=0 NormalZ=1 AngleXU=0 Radius=2.6 StartAngle=1.20535 EndAngle=4.03064
    g20: ArcOfCircle CenterX=39 CenterY=57.5 CenterZ=0 NormalX=0 NormalY=0 NormalZ=1 AngleXU=0 Radius=2.6 StartAngle=0.15815 EndAngle=2.98344
    g21: ArcOfCircle CenterX=50.6913 CenterY=50.75 CenterZ=0 NormalX=0 NormalY=0 NormalZ=1 AngleXU=0 Radius=2.6 StartAngle=5.39414 EndAngle=8.21943
    g22: ArcOfCircle CenterX=50.6913 CenterY=37.25 CenterZ=0 NormalX=0 NormalY=0 NormalZ=1 AngleXU=0 Radius=2.6 StartAngle=4.34694 EndAngle=7.17223
    g23: ArcOfCircle CenterX=39 CenterY=30.5 CenterZ=0 NormalX=0 NormalY=0 NormalZ=1 AngleXU=0 Radius=2.6 StartAngle=3.29974 EndAngle=6.12503
    g24: ArcOfCircle CenterX=27.3087 CenterY=37.25 CenterZ=0 NormalX=0 NormalY=0 NormalZ=1 AngleXU=0 Radius=2.6 StartAngle=2.25255 EndAngle=5.07784
    g25: ArcOfCircle CenterX=27.3087 CenterY=50.75 CenterZ=0 NormalX=0 NormalY=0 NormalZ=1 AngleXU=0 Radius=2.6 StartAngle=1.20535 EndAngle=4.03064
    g26: LineSegment [constr] StartX=-42.75 StartY=50.4952 StartZ=0 EndX=-46.5 EndY=44 EndZ=0
    g27: LineSegment [constr] StartX=-46.5 StartY=44 StartZ=0 EndX=-42.75 EndY=37.5048 EndZ=0
    g28: LineSegment [constr] StartX=-42.75 StartY=37.5048 StartZ=0 EndX=-35.25 EndY=37.5048 EndZ=0
    g29: LineSegment [constr] StartX=-35.25 StartY=37.5048 StartZ=0 EndX=-31.5 EndY=44 EndZ=0
    g30: LineSegment [constr] StartX=-31.5 StartY=44 StartZ=0 EndX=-35.25 EndY=50.4952 EndZ=0
    g31: LineSegment [constr] StartX=-35.25 StartY=50.4952 StartZ=0 EndX=-42.75 EndY=50.4952 EndZ=0
    g32: Circle [constr] CenterX=-39 CenterY=44 CenterZ=0 NormalX=0 NormalY=0 NormalZ=1 AngleXU=0 Radius=7.5
    g33: LineSegment [constr] StartX=42.75 StartY=50.4952 StartZ=0 EndX=35.25 EndY=50.4952 EndZ=0
    g34: LineSegment [constr] StartX=35.25 StartY=50.4952 StartZ=0 EndX=31.5 EndY=44 EndZ=0
    g35: LineSegment [constr] StartX=31.5 StartY=44 StartZ=0 EndX=35.25 EndY=37.5048 EndZ=0
    g36: LineSegment [constr] StartX=35.25 StartY=37.5048 StartZ=0 EndX=42.75 EndY=37.5048 EndZ=0
    g37: LineSegment [constr] StartX=42.75 StartY=37.5048 StartZ=0 EndX=46.5 EndY=44 EndZ=0
    g38: LineSegment [constr] StartX=46.5 StartY=44 StartZ=0 EndX=42.75 EndY=50.4952 EndZ=0
    g39: Circle [constr] CenterX=39 CenterY=44 CenterZ=0 NormalX=0 NormalY=0 NormalZ=1 AngleXU=0 Radius=7.5
    g40: LineSegment StartX=-49.7622 StartY=53.1783 StartZ=0 EndX=-42.75 EndY=50.4952 EndZ=0
    g41: LineSegment StartX=-41.5676 StartY=57.9095 StartZ=0 EndX=-42.75 EndY=50.4952 EndZ=0
    g42: LineSegment StartX=-36.4324 StartY=57.9095 StartZ=0 EndX=-35.25 EndY=50.4952 EndZ=0
    g43: LineSegment StartX=-35.25 StartY=50.4952 StartZ=0 EndX=-28.2378 EndY=53.1783 EndZ=0
    g44: LineSegment StartX=-25.6703 StartY=48.7312 StartZ=0 EndX=-31.5 EndY=44 EndZ=0
    g45: LineSegment StartX=-31.5 StartY=44 StartZ=0 EndX=-25.6703 EndY=39.2688 EndZ=0
    g46: LineSegment StartX=-28.2378 StartY=34.8217 StartZ=0 EndX=-35.25 EndY=37.5048 EndZ=0
    g47: LineSegment StartX=-35.25 StartY=37.5048 StartZ=0 EndX=-36.4324 EndY=30.0905 EndZ=0
    g48: LineSegment StartX=-41.5676 StartY=30.0905 StartZ=0 EndX=-42.75 EndY=37.5048 EndZ=0
    g49: LineSegment StartX=-42.75 StartY=37.5048 StartZ=0 EndX=-49.7622 EndY=34.8217 EndZ=0
    g50: LineSegment StartX=-52.3297 StartY=39.2688 StartZ=0 EndX=-46.5 EndY=44 EndZ=0
    g51: LineSegment StartX=-46.5 StartY=44 StartZ=0 EndX=-52.3297 EndY=48.7312 EndZ=0
    g52: LineSegment StartX=25.6703 StartY=48.7312 StartZ=0 EndX=31.5 EndY=44 EndZ=0
    g53: LineSegment StartX=31.5 StartY=44 StartZ=0 EndX=25.6703 EndY=39.2688 EndZ=0
    g54: LineSegment StartX=28.2378 StartY=34.8217 StartZ=0 EndX=35.25 EndY=37.5048 EndZ=0
    g55: LineSegment StartX=35.25 StartY=37.5048 StartZ=0 EndX=36.4324 EndY=30.0905 EndZ=0
    g56: LineSegment StartX=41.5676 StartY=30.0905 StartZ=0 EndX=42.75 EndY=37.5048 EndZ=0
    g57: LineSegment StartX=42.75 StartY=37.5048 StartZ=0 EndX=49.7622 EndY=34.8217 EndZ=0
    g58: LineSegment StartX=52.3297 StartY=39.2688 StartZ=0 EndX=46.5 EndY=44 EndZ=0
    g59: LineSegment StartX=46.5 StartY=44 StartZ=0 EndX=52.3297 EndY=48.7312 EndZ=0
    g60: LineSegment StartX=49.7622 StartY=53.1783 StartZ=0 EndX=42.75 EndY=50.4952 EndZ=0
    g61: LineSegment StartX=42.75 StartY=50.4952 StartZ=0 EndX=41.5676 EndY=57.9095 EndZ=0
    g62: LineSegment StartX=36.4324 StartY=57.9095 StartZ=0 EndX=35.25 EndY=50.4952 EndZ=0
    g63: LineSegment StartX=35.25 StartY=50.4952 StartZ=0 EndX=28.2378 EndY=53.1783 EndZ=0
  constraints (127):
    c: Coincident(g0,g1)
    c: Coincident(g1,g2)
    c: Coincident(g2,g3)
    c: Coincident(g3,g4)
    c: Coincident(g4,g5)
    c: Coincident(g5,g0)
    c: Equal(g0, g1-g5) x5
    c: PointOnObject(g0,g6)
    c: PointOnObject(g1,g6)
    c: PointOnObject(g2,g6)
    c: PointOnObject(g3,g6)
    c: PointOnObject(g4,g6)
    c: PointOnObject(g5,g6)
    c: Coincident(g7,g8)
    c: Coincident(g8,g9)
    c: Coincident(g9,g10)
    c: Coincident(g10,g11)
    c: Coincident(g11,g12)
    c: Coincident(g12,g7)
    c: Equal(g7, g8-g12) x5
    c: PointOnObject(g7,g13)
    c: PointOnObject(g8,g13)
    c: PointOnObject(g9,g13)
    c: PointOnObject(g10,g13)
    c: PointOnObject(g11,g13)
    c: PointOnObject(g12,g13)
    c: Coincident(g13,g-4)
    c: Coincident(g6,g-3)
    c: Equal(g6,g13)
    c: Vertical(g8)
    c: Vertical(g4)
    c: Radius(g6) = 13.5
    c: Coincident(g26,g27)
    c: Coincident(g27,g28)
    c: Coincident(g28,g29)
    c: Coincident(g29,g30)
    c: Coincident(g30,g31)
    c: Coincident(g31,g26)
    c: Equal(g26, g27-g31) x5
    c: PointOnObject(g26,g32)
    c: PointOnObject(g27,g32)
    c: PointOnObject(g28,g32)
    c: PointOnObject(g29,g32)
    c: PointOnObject(g30,g32)
    c: PointOnObject(g31,g32)
    c: Coincident(g32,g6)
    c: Coincident(g33,g34)
    c: Coincident(g34,g35)
    c: Coincident(g35,g36)
    c: Coincident(g36,g37)
    c: Coincident(g37,g38)
    c: Coincident(g38,g33)
    c: Equal(g33, g34-g38) x5
    c: PointOnObject(g33,g39)
    c: PointOnObject(g34,g39)
    c: PointOnObject(g35,g39)
    c: PointOnObject(g36,g39)
    c: PointOnObject(g37,g39)
    c: PointOnObject(g38,g39)
    c: Coincident(g13,g39)
    c: Equal(g32,g39)
    c: Radius(g39) = 7.5
    c: Horizontal(g31)
    c: Horizontal(g33)
    c: Coincident(g40,g26)
    c: Coincident(g41,g40)
    c: Coincident(g42,g30)
    c: Coincident(g43,g42)
    c: Coincident(g44,g29)
    c: Coincident(g45,g44)
    c: Coincident(g46,g28)
    c: Coincident(g47,g46)
    c: Coincident(g48,g27)
    c: Coincident(g49,g48)
    c: Coincident(g50,g26)
    c: Coincident(g51,g50)
    c: Coincident(g52,g34)
    c: Coincident(g53,g52)
    c: Coincident(g54,g35)
    c: Coincident(g55,g54)
    c: Coincident(g56,g36)
    c: Coincident(g57,g56)
    c: Coincident(g58,g37)
    c: Coincident(g59,g58)
    c: Coincident(g60,g33)
    c: Coincident(g61,g60)
    c: Coincident(g62,g33)
    c: Coincident(g63,g62)
    c: Radius(g19) = 2.6
    c: Equal(g19, g14-g18) x5
    c: Equal(g19, g20-g25) x6
    c: Tangent(g42,g14) = 1.5708
    c: Tangent(g43,g15) = 1.5708
    c: Tangent(g44,g15) = 1.5708
    c: Tangent(g45,g16) = 1.5708
    c: Tangent(g46,g16) = 1.5708
    c: Tangent(g47,g17) = 1.5708
    c: Tangent(g48,g17) = 1.5708
    c: Tangent(g49,g18) = 1.5708
    c: Tangent(g50,g18) = 1.5708
    c: Tangent(g51,g19) = 1.5708
    c: Tangent(g40,g19) = 1.5708
    c: Tangent(g41,g14) = -1.5708
    c: Tangent(g61,g20) = -1.5708
    c: Tangent(g60,g21) = -1.5708
    c: Tangent(g59,g21) = -1.5708
    c: Tangent(g58,g22) = -1.5708
    c: Tangent(g57,g22) = -1.5708
    c: Tangent(g56,g23) = -1.5708
    c: Tangent(g55,g23) = -1.5708
    c: Tangent(g54,g24) = -1.5708
    c: Tangent(g53,g24) = -1.5708
    c: Tangent(g52,g25) = -1.5708
    c: Tangent(g63,g25) = -1.5708
    c: Tangent(g62,g20) = -1.5708
    c: Coincident(g20,g7)
    c: Coincident(g21,g11)
    c: Coincident(g22,g10)
    c: Coincident(g23,g9)
    c: Coincident(g24,g8)
    c: Coincident(g25,g7)
    c: Coincident(g14,g0)
    c: Coincident(g15,g4)
    c: Coincident(g16,g3)
    c: Coincident(g17,g2)
    c: Coincident(g18,g1)
    c: Coincident(g19,g0)
FEATURE [PartDesign::Pocket] Pocket004  label="Servohorn Mount"
  BaseFeature = -> Pocket003
  Length = 2
  Length2 = 100
  Profile = -> Sketch2049
  Type = 0
FEATURE [Sketcher::SketchObject] Sketch2050
  ExternalGeometry = -> [Pocket004]
  MapMode = 5
  Placement = pos=(0,0,3) rot=(0,0,1;0rad)
  Support = -> [Pocket004]
  sketch-geometry (26):
    g0: LineSegment [constr] StartX=-39 StartY=54.5 StartZ=0 EndX=-48.0933 EndY=49.25 EndZ=0
    g1: LineSegment [constr] StartX=-48.0933 StartY=49.25 StartZ=0 EndX=-48.0933 EndY=38.75 EndZ=0
    g2: LineSegment [constr] StartX=-48.0933 StartY=38.75 StartZ=0 EndX=-39 EndY=33.5 EndZ=0
    g3: LineSegment [constr] StartX=-39 StartY=33.5 StartZ=0 EndX=-29.9067 EndY=38.75 EndZ=0
    g4: LineSegment [constr] StartX=-29.9067 StartY=38.75 StartZ=0 EndX=-29.9067 EndY=49.25 EndZ=0
    g5: LineSegment [constr] StartX=-29.9067 StartY=49.25 StartZ=0 EndX=-39 EndY=54.5 EndZ=0
    g6: Circle [constr] CenterX=-39 CenterY=44 CenterZ=0 NormalX=0 NormalY=0 NormalZ=1 AngleXU=0 Radius=10.5
    g7: LineSegment [constr] StartX=39 StartY=54.5 StartZ=0 EndX=29.9067 EndY=49.25 EndZ=0
    g8: LineSegment [constr] StartX=29.9067 StartY=49.25 StartZ=0 EndX=29.9067 EndY=38.75 EndZ=0
    g9: LineSegment [constr] StartX=29.9067 StartY=38.75 StartZ=0 EndX=39 EndY=33.5 EndZ=0
    g10: LineSegment [constr] StartX=39 StartY=33.5 StartZ=0 EndX=48.0933 EndY=38.75 EndZ=0
    g11: LineSegment [constr] StartX=48.0933 StartY=38.75 StartZ=0 EndX=48.0933 EndY=49.25 EndZ=0
    g12: LineSegment [constr] StartX=48.0933 StartY=49.25 StartZ=0 EndX=39 EndY=54.5 EndZ=0
    g13: Circle [constr] CenterX=39 CenterY=44 CenterZ=0 NormalX=0 NormalY=0 NormalZ=1 AngleXU=0 Radius=10.5
    g14: Circle CenterX=-39 CenterY=54.5 CenterZ=0 NormalX=0 NormalY=0 NormalZ=1 AngleXU=0 Radius=0.95
    g15: Circle CenterX=-29.9067 CenterY=49.25 CenterZ=0 NormalX=0 NormalY=0 NormalZ=1 AngleXU=0 Radius=0.95
    g16: Circle CenterX=-29.9067 CenterY=38.75 CenterZ=0 NormalX=0 NormalY=0 NormalZ=1 AngleXU=0 Radius=0.95
    g17: Circle CenterX=-39 CenterY=33.5 CenterZ=0 NormalX=0 NormalY=0 NormalZ=1 AngleXU=0 Radius=0.95
    g18: Circle CenterX=-48.0933 CenterY=38.75 CenterZ=0 NormalX=0 NormalY=0 NormalZ=1 AngleXU=0 Radius=0.95
    g19: Circle CenterX=-48.0933 CenterY=49.25 CenterZ=0 NormalX=0 NormalY=0 NormalZ=1 AngleXU=0 Radius=0.95
    g20: Circle CenterX=29.9067 CenterY=49.25 CenterZ=0 NormalX=0 NormalY=0 NormalZ=1 AngleXU=0 Radius=0.95
    g21: Circle CenterX=39 CenterY=54.5 CenterZ=0 NormalX=0 NormalY=0 NormalZ=1 AngleXU=0 Radius=0.95
    g22: Circle CenterX=48.0933 CenterY=49.25 CenterZ=0 NormalX=0 NormalY=0 NormalZ=1 AngleXU=0 Radius=0.95
    g23: Circle CenterX=48.0933 CenterY=38.75 CenterZ=0 NormalX=0 NormalY=0 NormalZ=1 AngleXU=0 Radius=0.95
    g24: Circle CenterX=39 CenterY=33.5 CenterZ=0 NormalX=0 NormalY=0 NormalZ=1 AngleXU=0 Radius=0.95
    g25: Circle CenterX=29.9067 CenterY=38.75 CenterZ=0 NormalX=0 NormalY=0 NormalZ=1 AngleXU=0 Radius=0.95
  constraints (48):
    c: Coincident(g0,g1)
    c: Coincident(g1,g2)
    c: Coincident(g2,g3)
    c: Coincident(g3,g4)
    c: Coincident(g4,g5)
    c: Coincident(g5,g0)
    c: Equal(g0, g1-g5) x5
    c: PointOnObject(g0,g6)
    c: PointOnObject(g1,g6)
    c: PointOnObject(g2,g6)
    c: PointOnObject(g3,g6)
    c: PointOnObject(g4,g6)
    c: PointOnObject(g5,g6)
    c: Coincident(g6,g-3)
    c: Coincident(g7,g8)
    c: Coincident(g8,g9)
    c: Coincident(g9,g10)
    c: Coincident(g10,g11)
    c: Coincident(g11,g12)
    c: Coincident(g12,g7)
    c: Equal(g7, g8-g12) x5
    c: PointOnObject(g7,g13)
    c: PointOnObject(g8,g13)
    c: PointOnObject(g9,g13)
    c: PointOnObject(g10,g13)
    c: PointOnObject(g11,g13)
    c: PointOnObject(g12,g13)
    c: Coincident(g13,g-4)
    c: Vertical(g4)
    c: Vertical(g8)
    c: Equal(g13,g6)
    c: Radius(g6) = 10.5
    c: Coincident(g14,g0)
    c: Coincident(g15,g4)
    c: Coincident(g16,g3)
    c: Coincident(g17,g2)
    c: Coincident(g18,g1)
    c: Coincident(g19,g0)
    c: Coincident(g20,g7)
    c: Coincident(g21,g7)
    c: Coincident(g22,g11)
    c: Coincident(g23,g10)
    c: Coincident(g24,g9)
    c: Coincident(g25,g8)
    c: Radius(g20) = 0.95
    c: Equal(g20, g21-g25) x5
    c: Equal(g20, g15-g19) x5
    c: Equal(g20,g14)
FEATURE [PartDesign::Pocket] Pocket745  label="Servohorn Screws"
  BaseFeature = -> Pocket004
  Length = 3
  Length2 = 100
  Profile = -> Sketch2050
  Type = 0
FEATURE [PartDesign::Fillet] Fillet  label="Servohorn Fillet"
  Base = -> Pocket745 [Edge214,Edge184,Edge190,Edge208,Edge174,Edge143,Edge168,Edge150,Edge202,Edge196,Edge162,Edge156]
  BaseFeature = -> Pocket745
  Radius = 1
FEATURE [PartDesign::Body] Body  label="Outer_Shoulder"
  Group = -> [Sketch,Pad,Sketch001,Pocket,Sketch2046,Pocket001,Sketch2048,Pocket002,Sketch2047,Pocket003,Sketch2049,Pocket004,Sketch2050,Pocket745,Fillet]
  Origin = -> Origin799
  Placement = pos=(114.75,-99.65,166.6) rot=(0.57735,0.57735,0.57735;2.0944rad)
  Tip = -> Fillet
FEATURE [Sketcher::SketchObject] Sketch2055
  MapMode = 5
  Support = -> [XY_Plane801]
  sketch-geometry (64):
    g0: LineSegment [constr] StartX=-3.75 StartY=6.49519 StartZ=0 EndX=-7.5 EndY=0 EndZ=0
    g1: LineSegment [constr] StartX=-7.5 StartY=0 StartZ=0 EndX=-3.75 EndY=-6.49519 EndZ=0
    g2: LineSegment [constr] StartX=-3.75 StartY=-6.49519 StartZ=0 EndX=3.75 EndY=-6.49519 EndZ=0
    g3: LineSegment [constr] StartX=3.75 StartY=-6.49519 StartZ=0 EndX=7.5 EndY=0 EndZ=0
    g4: LineSegment [constr] StartX=7.5 StartY=0 StartZ=0 EndX=3.75 EndY=6.49519 EndZ=0
    g5: LineSegment [constr] StartX=3.75 StartY=6.49519 StartZ=0 EndX=-3.75 EndY=6.49519 EndZ=0
    g6: Circle [constr] CenterX=0 CenterY=0 CenterZ=0 NormalX=0 NormalY=0 NormalZ=1 AngleXU=0 Radius=7.5
    g7: LineSegment [constr] StartX=0 StartY=7.5 StartZ=0 EndX=-6.49519 EndY=3.75 EndZ=0
    g8: LineSegment [constr] StartX=-6.49519 StartY=3.75 StartZ=0 EndX=-6.49519 EndY=-3.75 EndZ=0
    g9: LineSegment [constr] StartX=-6.49519 StartY=-3.75 StartZ=0 EndX=9.8e-15 EndY=-7.5 EndZ=0
    g10: LineSegment [constr] StartX=9.8e-15 StartY=-7.5 StartZ=0 EndX=6.49519 EndY=-3.75 EndZ=0
    g11: LineSegment [constr] StartX=6.49519 StartY=-3.75 StartZ=0 EndX=6.49519 EndY=3.75 EndZ=0
    g12: LineSegment [constr] StartX=6.49519 StartY=3.75 StartZ=0 EndX=0 EndY=7.5 EndZ=0
    g13: Circle [constr] CenterX=0 CenterY=0 CenterZ=0 NormalX=0 NormalY=0 NormalZ=1 AngleXU=0 Radius=7.5
    g14: LineSegment [constr] StartX=0 StartY=10.5 StartZ=0 EndX=-9.09327 EndY=5.25 EndZ=0
    g15: LineSegment [constr] StartX=-9.09327 StartY=5.25 StartZ=0 EndX=-9.09327 EndY=-5.25 EndZ=0
    g16: LineSegment [constr] StartX=-9.09327 StartY=-5.25 StartZ=0 EndX=-1.42e-14 EndY=-10.5 EndZ=0
    g17: LineSegment [constr] StartX=-1.42e-14 StartY=-10.5 StartZ=0 EndX=9.09327 EndY=-5.25 EndZ=0
    g18: LineSegment [constr] StartX=9.09327 StartY=-5.25 StartZ=0 EndX=9.09327 EndY=5.25 EndZ=0
    g19: LineSegment [constr] StartX=9.09327 StartY=5.25 StartZ=0 EndX=0 EndY=10.5 EndZ=0
    g20: Circle [constr] CenterX=0 CenterY=0 CenterZ=0 NormalX=0 NormalY=0 NormalZ=1 AngleXU=0 Radius=10.5
    g21: LineSegment [constr] StartX=0 StartY=13.5 StartZ=0 EndX=-11.6913 EndY=6.75 EndZ=0
    g22: LineSegment [constr] StartX=-11.6913 StartY=6.75 StartZ=0 EndX=-11.6913 EndY=-6.75 EndZ=0
    g23: LineSegment [constr] StartX=-11.6913 StartY=-6.75 StartZ=0 EndX=0 EndY=-13.5 EndZ=0
    g24: LineSegment [constr] StartX=0 StartY=-13.5 StartZ=0 EndX=11.6913 EndY=-6.75 EndZ=0
    g25: LineSegment [constr] StartX=11.6913 StartY=-6.75 StartZ=0 EndX=11.6913 EndY=6.75 EndZ=0
    g26: LineSegment [constr] StartX=11.6913 StartY=6.75 StartZ=0 EndX=0 EndY=13.5 EndZ=0
    g27: Circle [constr] CenterX=0 CenterY=0 CenterZ=0 NormalX=0 NormalY=0 NormalZ=1 AngleXU=0 Radius=13.5
    g28: ArcOfCircle CenterX=0 CenterY=13.5 CenterZ=0 NormalX=0 NormalY=0 NormalZ=1 AngleXU=0 Radius=2.5 StartAngle=0.171439 EndAngle=2.97015
    g29: ArcOfCircle CenterX=11.6913 CenterY=6.75 CenterZ=0 NormalX=0 NormalY=0 NormalZ=1 AngleXU=0 Radius=2.5 StartAngle=5.40743 EndAngle=8.20614
    g30: ArcOfCircle CenterX=11.6913 CenterY=-6.75 CenterZ=0 NormalX=0 NormalY=0 NormalZ=1 AngleXU=0 Radius=2.5 StartAngle=4.36023 EndAngle=7.15894
    g31: ArcOfCircle CenterX=0 CenterY=-13.5 CenterZ=0 NormalX=0 NormalY=0 NormalZ=1 AngleXU=0 Radius=2.5 StartAngle=3.31303 EndAngle=6.11175
    g32: ArcOfCircle CenterX=-11.6913 CenterY=-6.75 CenterZ=0 NormalX=0 NormalY=0 NormalZ=1 AngleXU=0 Radius=2.5 StartAngle=2.26583 EndAngle=5.06455
    g33: ArcOfCircle CenterX=-11.6913 CenterY=6.75 CenterZ=0 NormalX=0 NormalY=0 NormalZ=1 AngleXU=0 Radius=2.5 StartAngle=1.21864 EndAngle=4.01735
    g34: LineSegment StartX=-10.829 StartY=9.09658 StartZ=0 EndX=-3.75 EndY=6.49519 EndZ=0
    g35: LineSegment StartX=-3.75 StartY=6.49519 StartZ=0 EndX=-2.46335 EndY=13.9265 EndZ=0
    g36: LineSegment StartX=2.46335 StartY=13.9265 StartZ=0 EndX=3.75 EndY=6.49519 EndZ=0
    g37: LineSegment StartX=3.75 StartY=6.49519 StartZ=0 EndX=10.829 EndY=9.09658 EndZ=0
    g38: LineSegment StartX=13.2924 StartY=4.82993 StartZ=0 EndX=7.5 EndY=0 EndZ=0
    g39: LineSegment StartX=7.5 StartY=0 StartZ=0 EndX=13.2924 EndY=-4.82993 EndZ=0
    g40: LineSegment StartX=10.829 StartY=-9.09658 StartZ=0 EndX=3.75 EndY=-6.49519 EndZ=0
    g41: LineSegment StartX=3.75 StartY=-6.49519 StartZ=0 EndX=2.46335 EndY=-13.9265 EndZ=0
    g42: LineSegment StartX=-2.46335 StartY=-13.9265 StartZ=0 EndX=-3.75 EndY=-6.49519 EndZ=0
    g43: LineSegment StartX=-3.75 StartY=-6.49519 StartZ=0 EndX=-10.829 EndY=-9.09658 EndZ=0
    g44: LineSegment StartX=-13.2924 StartY=-4.82993 StartZ=0 EndX=-7.5 EndY=0 EndZ=0
    g45: LineSegment StartX=-7.5 StartY=0 StartZ=0 EndX=-13.2924 EndY=4.82993 EndZ=0
    g46: Circle CenterX=-11.6913 CenterY=6.75 CenterZ=0 NormalX=0 NormalY=0 NormalZ=1 AngleXU=0 Radius=0.75
    g47: Circle CenterX=-9.09327 CenterY=5.25 CenterZ=0 NormalX=0 NormalY=0 NormalZ=1 AngleXU=0 Radius=0.75
    g48: Circle CenterX=-6.49519 CenterY=3.75 CenterZ=0 NormalX=0 NormalY=0 NormalZ=1 AngleXU=0 Radius=0.75
    g49: Circle CenterX=0 CenterY=13.5 CenterZ=0 NormalX=0 NormalY=0 NormalZ=1 AngleXU=0 Radius=0.75
    g50: Circle CenterX=0 CenterY=10.5 CenterZ=0 NormalX=0 NormalY=0 NormalZ=1 AngleXU=0 Radius=0.75
    g51: Circle CenterX=0 CenterY=7.5 CenterZ=0 NormalX=0 NormalY=0 NormalZ=1 AngleXU=0 Radius=0.75
    g52: Circle CenterX=11.6913 CenterY=6.75 CenterZ=0 NormalX=0 NormalY=0 NormalZ=1 AngleXU=0 Radius=0.75
    g53: Circle CenterX=9.09327 CenterY=5.25 CenterZ=0 NormalX=0 NormalY=0 NormalZ=1 AngleXU=0 Radius=0.75
    g54: Circle CenterX=6.49519 CenterY=3.75 CenterZ=0 NormalX=0 NormalY=0 NormalZ=1 AngleXU=0 Radius=0.75
    g55: Circle CenterX=11.6913 CenterY=-6.75 CenterZ=0 NormalX=0 NormalY=0 NormalZ=1 AngleXU=0 Radius=0.75
    g56: Circle CenterX=9.09327 CenterY=-5.25 CenterZ=0 NormalX=0 NormalY=0 NormalZ=1 AngleXU=0 Radius=0.75
    g57: Circle CenterX=6.49519 CenterY=-3.75 CenterZ=0 NormalX=0 NormalY=0 NormalZ=1 AngleXU=0 Radius=0.75
    g58: Circle CenterX=9.8e-15 CenterY=-7.5 CenterZ=0 NormalX=0 NormalY=0 NormalZ=1 AngleXU=0 Radius=0.75
    g59: Circle CenterX=-1.42e-14 CenterY=-10.5 CenterZ=0 NormalX=0 NormalY=0 NormalZ=1 AngleXU=0 Radius=0.75
    g60: Circle CenterX=0 CenterY=-13.5 CenterZ=0 NormalX=0 NormalY=0 NormalZ=1 AngleXU=0 Radius=0.75
    g61: Circle CenterX=-11.6913 CenterY=-6.75 CenterZ=0 NormalX=0 NormalY=0 NormalZ=1 AngleXU=0 Radius=0.75
    g62: Circle CenterX=-9.09327 CenterY=-5.25 CenterZ=0 NormalX=0 NormalY=0 NormalZ=1 AngleXU=0 Radius=0.75
    g63: Circle CenterX=-6.49519 CenterY=-3.75 CenterZ=0 NormalX=0 NormalY=0 NormalZ=1 AngleXU=0 Radius=0.75
  constraints (136):
    c: Coincident(g0,g1)
    c: Coincident(g1,g2)
    c: Coincident(g2,g3)
    c: Coincident(g3,g4)
    c: Coincident(g4,g5)
    c: Coincident(g5,g0)
    c: Equal(g0, g1-g5) x5
    c: PointOnObject(g0,g6)
    c: PointOnObject(g1,g6)
    c: PointOnObject(g2,g6)
    c: PointOnObject(g3,g6)
    c: PointOnObject(g4,g6)
    c: PointOnObject(g5,g6)
    c: Coincident(g6,g-1)
    c: Coincident(g7,g8)
    c: Coincident(g8,g9)
    c: Coincident(g9,g10)
    c: Coincident(g10,g11)
    c: Coincident(g11,g12)
    c: Coincident(g12,g7)
    c: Equal(g7, g8-g12) x5
    c: PointOnObject(g7,g13)
    c: PointOnObject(g8,g13)
    c: PointOnObject(g9,g13)
    c: PointOnObject(g10,g13)
    c: PointOnObject(g11,g13)
    c: PointOnObject(g12,g13)
    c: Coincident(g13,g-1)
    c: PointOnObject(g12,g6)
    c: PointOnObject(g7,g-2)
    c: Horizontal(g5)
    c: Radius(g6) = 7.5
    c: Coincident(g14,g15)
    c: Coincident(g15,g16)
    c: Coincident(g16,g17)
    c: Coincident(g17,g18)
    c: Coincident(g18,g19)
    c: Coincident(g19,g14)
    c: Equal(g14, g15-g19) x5
    c: PointOnObject(g14,g20)
    c: PointOnObject(g15,g20)
    c: PointOnObject(g16,g20)
    c: PointOnObject(g17,g20)
    c: PointOnObject(g18,g20)
    c: PointOnObject(g19,g20)
    c: Coincident(g20,g-1)
    c: PointOnObject(g19,g-2)
    c: Radius(g20) = 10.5
    c: Coincident(g21,g22)
    c: Coincident(g22,g23)
    c: Coincident(g23,g24)
    c: Coincident(g24,g25)
    c: Coincident(g25,g26)
    c: Coincident(g26,g21)
    c: Equal(g21, g22-g26) x5
    c: PointOnObject(g21,g27)
    c: PointOnObject(g22,g27)
    c: PointOnObject(g23,g27)
    c: PointOnObject(g24,g27)
    c: PointOnObject(g25,g27)
    c: PointOnObject(g26,g27)
    c: Coincident(g27,g-1)
    c: PointOnObject(g26,g-2)
    c: Radius(g27) = 13.5
    c: Coincident(g28,g21)
    c: Coincident(g29,g25)
    c: Coincident(g30,g24)
    c: Coincident(g31,g23)
    c: Coincident(g32,g22)
    c: Coincident(g33,g21)
    c: Coincident(g34,g0)
    c: Coincident(g35,g34)
    c: Coincident(g36,g4)
    c: Coincident(g37,g36)
    c: Coincident(g38,g3)
    c: Coincident(g39,g38)
    c: Coincident(g40,g2)
    c: Coincident(g41,g40)
    c: Coincident(g42,g1)
    c: Coincident(g43,g42)
    c: Coincident(g44,g0)
    c: Coincident(g45,g44)
    c: Tangent(g35,g28) = 1.5708
    c: Tangent(g36,g28) = 1.5708
    c: Tangent(g37,g29) = 1.5708
    c: Tangent(g38,g29) = 1.5708
    c: Tangent(g39,g30) = 1.5708
    c: Tangent(g40,g30) = 1.5708
    c: Tangent(g41,g31) = 1.5708
    c: Tangent(g42,g31) = 1.5708
    c: Tangent(g43,g32) = 1.5708
    c: Tangent(g44,g32) = 1.5708
    c: Tangent(g45,g33) = 1.5708
    c: Tangent(g34,g33) = 1.5708
    c: Radius(g29) = 2.5
    c: Equal(g29,g28)
    c: Equal(g28,g33)
    c: Equal(g33,g32)
    c: Equal(g32,g31)
    c: Equal(g31,g30)
    c: Coincident(g46,g33)
    c: Coincident(g47,g14)
    c: Coincident(g48,g7)
    c: Coincident(g49,g28)
    c: Coincident(g50,g14)
    c: Coincident(g51,g7)
    c: Coincident(g52,g29)
    c: Coincident(g53,g18)
    c: Coincident(g54,g11)
    c: Coincident(g55,g30)
    c: Coincident(g56,g17)
    c: Coincident(g57,g10)
    c: Coincident(g58,g9)
    c: Coincident(g59,g16)
    c: Coincident(g60,g31)
    c: Coincident(g61,g32)
    c: Coincident(g62,g15)
    c: Coincident(g63,g8)
    c: Equal(g61,g62)
    c: Equal(g62,g63)
    c: Equal(g63,g58)
    c: Equal(g58,g59)
    c: Equal(g59,g60)
    c: Equal(g60,g55)
    c: Equal(g55,g56)
    c: Equal(g56,g57)
    c: Equal(g57,g54)
    c: Equal(g54,g53)
    c: Equal(g53,g52)
    c: Equal(g52,g51)
    c: Equal(g51,g50)
    c: Equal(g50,g49)
    c: Equal(g49,g46)
    c: Equal(g46,g47)
    c: Equal(g47,g48)
    c: Radius(g55) = 0.75
FEATURE [PartDesign::Pad] Pad900
  Length = 2
  Length2 = 100
  Profile = -> Sketch2055
  Type = 0
FEATURE [Sketcher::SketchObject] Sketch2051
  MapMode = 5
  Placement = pos=(0,0,2) rot=(0,0,1;0rad)
  Support = -> [Pad900]
  sketch-geometry (2):
    g0: Circle CenterX=0 CenterY=0 CenterZ=0 NormalX=0 NormalY=0 NormalZ=1 AngleXU=0 Radius=5
    g1: Circle CenterX=0 CenterY=0 CenterZ=0 NormalX=0 NormalY=0 NormalZ=1 AngleXU=0 Radius=3.5
  constraints (4):
    c: Coincident(g0,g-1)
    c: Coincident(g1,g0)
    c: Radius(g1) = 3.5
    c: Radius(g0) = 5
FEATURE [PartDesign::Pocket] Pocket746
  BaseFeature = -> Pad900
  Length = 1
  Length2 = 100
  Profile = -> Sketch2051
  Type = 0
FEATURE [Sketcher::SketchObject] Sketch2052
  MapMode = 5
  Placement = pos=(0,0,2) rot=(0,0,1;0rad)
  Support = -> [Pocket746]
  sketch-geometry (1):
    g0: Circle CenterX=0 CenterY=0 CenterZ=0 NormalX=0 NormalY=0 NormalZ=1 AngleXU=0 Radius=3
  constraints (2):
    c: Coincident(g0,g-1)
    c: Radius(g0) = 3
FEATURE [PartDesign::Pocket] Pocket747
  BaseFeature = -> Pocket746
  Length = 1
  Length2 = 100
  Profile = -> Sketch2052
  Type = 0
FEATURE [Sketcher::SketchObject] Sketch2054
  MapMode = 5
  Placement = pos=(0,0,1) rot=(0,0,1;0rad)
  Support = -> [Pocket747]
  sketch-geometry (1):
    g0: Circle CenterX=0 CenterY=0 CenterZ=0 NormalX=0 NormalY=0 NormalZ=1 AngleXU=0 Radius=1.5
  constraints (2):
    c: Coincident(g0,g-1)
    c: Radius(g0) = 1.5
FEATURE [PartDesign::Pocket] Pocket748
  BaseFeature = -> Pocket747
  Length = 5
  Length2 = 100
  Profile = -> Sketch2054
  Type = 0
FEATURE [Sketcher::SketchObject] Sketch2053
  MapMode = 5
  Placement = pos=(0,0,0) rot=(1,0,0;3.14159rad)
  Support = -> [Pocket748]
  sketch-geometry (2):
    g0: Circle CenterX=0 CenterY=0 CenterZ=0 NormalX=0 NormalY=0 NormalZ=1 AngleXU=0 Radius=4.5
    g1: Circle CenterX=0 CenterY=0 CenterZ=0 NormalX=0 NormalY=0 NormalZ=1 AngleXU=0 Radius=3
  constraints (4):
    c: Coincident(g0,g-1)
    c: Coincident(g1,g0)
    c: Radius(g0) = 4.5
    c: Radius(g1) = 3
FEATURE [PartDesign::Pad] Pad899
  BaseFeature = -> Pocket748
  Length = 3
  Length2 = 100
  Profile = -> Sketch2053
  Type = 0
FEATURE [PartDesign::Fillet] Fillet250
  Base = -> Pad899 [Face5,Edge96,Face4]
  BaseFeature = -> Pad899
  Radius = 0.2
FEATURE [PartDesign::Body] Body572  label="Futuba FSH6B010"
  Group = -> [Sketch2055,Pad900,Sketch2051,Pocket746,Sketch2052,Pocket747,Sketch2054,Pocket748,Sketch2053,Pad899,Fillet250]
  Origin = -> Origin804
  Tip = -> Fillet250
FEATURE [App::Part] Part226  label="Servohorn017"
  Group = -> [Body572]
  Origin = -> Origin803
  Placement = pos=(0,0,-67) rot=(0,0,1;0rad)
FEATURE [Sketcher::SketchObject] Sketch2056
  MapMode = 5
  Support = -> [XY_Plane820]
FEATURE [Sketcher::SketchObject] Sketch2057
  MapMode = 5
  Support = -> [XY_Plane818]
  sketch-geometry (1):
    g0: Circle CenterX=0 CenterY=0 CenterZ=0 NormalX=0 NormalY=0 NormalZ=1 AngleXU=0 Radius=1.9
  constraints (2):
    c: Coincident(g0,g-1)
    c: Radius(g0) = 1.9
FEATURE [PartDesign::Pad] Pad911  label="M3x8 Head116"
  Length = 2
  Length2 = 100
  Profile = -> Sketch2057
  Type = 0
FEATURE [Sketcher::SketchObject] Sketch2059
  MapMode = 5
  Placement = pos=(0,0,2) rot=(0,0,1;0rad)
  Support = -> [Pad911]
  sketch-geometry (1):
    g0: Circle CenterX=0 CenterY=0 CenterZ=0 NormalX=0 NormalY=0 NormalZ=1 AngleXU=0 Radius=1
  constraints (2):
    c: Coincident(g0,g-1)
    c: Radius(g0) = 1
FEATURE [PartDesign::Pad] Pad912  label="M3x8 Thread116"
  BaseFeature = -> Pad911
  Length = 8
  Length2 = 100
  Profile = -> Sketch2059
  Type = 0
FEATURE [Sketcher::SketchObject] Sketch2060
  MapMode = 5
  Placement = pos=(0,0,0) rot=(1,0,0;3.14159rad)
  Support = -> [Pad912]
  sketch-geometry (7):
    g0: LineSegment StartX=0.77 StartY=0.44456 StartZ=0 EndX=0 EndY=0.889119 EndZ=0
    g1: LineSegment StartX=0 StartY=0.889119 StartZ=0 EndX=-0.77 EndY=0.44456 EndZ=0
    g2: LineSegment StartX=-0.77 StartY=0.44456 StartZ=0 EndX=-0.77 EndY=-0.44456 EndZ=0
    g3: LineSegment StartX=-0.77 StartY=-0.44456 StartZ=0 EndX=3.85628e-11 EndY=-0.889119 EndZ=0
    g4: LineSegment StartX=3.85628e-11 StartY=-0.889119 StartZ=0 EndX=0.77 EndY=-0.44456 EndZ=0
    g5: LineSegment StartX=0.77 StartY=-0.44456 StartZ=0 EndX=0.77 EndY=0.44456 EndZ=0
    g6: Circle [constr] CenterX=0 CenterY=0 CenterZ=0 NormalX=0 NormalY=0 NormalZ=1 AngleXU=0 Radius=0.889119
  constraints (16):
    c: Coincident(g0,g1)
    c: Coincident(g1,g2)
    c: Coincident(g2,g3)
    c: Coincident(g3,g4)
    c: Coincident(g4,g5)
    c: Coincident(g5,g0)
    c: Equal(g0, g1-g5) x5
    c: PointOnObject(g0,g6)
    c: PointOnObject(g1,g6)
    c: PointOnObject(g2,g6)
    c: PointOnObject(g3,g6)
    c: PointOnObject(g4,g6)
    c: PointOnObject(g5,g6)
    c: Coincident(g6,g-1)
    c: PointOnObject(g0,g-2)
    c: DistanceX(g1,g0) = 1.54
FEATURE [PartDesign::Pocket] Pocket750  label="M3x8 Wrench114"
  BaseFeature = -> Pad912
  Length = 1
  Length2 = 100
  Profile = -> Sketch2060
  Type = 0
FEATURE [Sketcher::SketchObject] Sketch2061
  MapMode = 5
  Support = -> [XY_Plane820]
FEATURE [Sketcher::SketchObject] Sketch2062
  MapMode = 5
  Support = -> [XY_Plane806]
  sketch-geometry (8):
    g0: LineSegment StartX=0 StartY=2.3094 StartZ=0 EndX=-2 EndY=1.1547 EndZ=0
    g1: LineSegment StartX=-2 StartY=1.1547 StartZ=0 EndX=-2 EndY=-1.1547 EndZ=0
    g2: LineSegment StartX=-2 StartY=-1.1547 StartZ=0 EndX=-2e-16 EndY=-2.3094 EndZ=0
    g3: LineSegment StartX=-2e-16 StartY=-2.3094 StartZ=0 EndX=2 EndY=-1.1547 EndZ=0
    g4: LineSegment StartX=2 StartY=-1.1547 StartZ=0 EndX=2 EndY=1.1547 EndZ=0
    g5: LineSegment StartX=2 StartY=1.1547 StartZ=0 EndX=0 EndY=2.3094 EndZ=0
    g6: Circle [constr] CenterX=0 CenterY=0 CenterZ=0 NormalX=0 NormalY=0 NormalZ=1 AngleXU=0 Radius=2.3094
    g7: Circle CenterX=0 CenterY=0 CenterZ=0 NormalX=0 NormalY=0 NormalZ=1 AngleXU=0 Radius=1
  constraints (18):
    c: Coincident(g0,g1)
    c: Coincident(g1,g2)
    c: Coincident(g2,g3)
    c: Coincident(g3,g4)
    c: Coincident(g4,g5)
    c: Coincident(g5,g0)
    c: Equal(g0, g1-g5) x5
    c: PointOnObject(g0,g6)
    c: PointOnObject(g1,g6)
    c: PointOnObject(g2,g6)
    c: PointOnObject(g3,g6)
    c: PointOnObject(g4,g6)
    c: PointOnObject(g5,g6)
    c: Coincident(g6,g-1)
    c: PointOnObject(g5,g-2)
    c: DistanceX(g0,g4) = 4
    c: Coincident(g7,g-1)
    c: Radius(g7) = 1
FEATURE [PartDesign::Pad] Pad906  label="M3 Nut Primitive180"
  Length = 0.6
  Length2 = 0.6
  Profile = -> Sketch2062
  Type = 4
FEATURE [Sketcher::SketchObject] Sketch2063
  MapMode = 5
  Support = -> [XY_Plane820]
  sketch-geometry (8):
    g0: LineSegment StartX=0 StartY=2.3094 StartZ=0 EndX=-2 EndY=1.1547 EndZ=0
    g1: LineSegment StartX=-2 StartY=1.1547 StartZ=0 EndX=-2 EndY=-1.1547 EndZ=0
    g2: LineSegment StartX=-2 StartY=-1.1547 StartZ=0 EndX=-2e-16 EndY=-2.3094 EndZ=0
    g3: LineSegment StartX=-2e-16 StartY=-2.3094 StartZ=0 EndX=2 EndY=-1.1547 EndZ=0
    g4: LineSegment StartX=2 StartY=-1.1547 StartZ=0 EndX=2 EndY=1.1547 EndZ=0
    g5: LineSegment StartX=2 StartY=1.1547 StartZ=0 EndX=0 EndY=2.3094 EndZ=0
    g6: Circle [constr] CenterX=0 CenterY=0 CenterZ=0 NormalX=0 NormalY=0 NormalZ=1 AngleXU=0 Radius=2.3094
    g7: Circle CenterX=0 CenterY=0 CenterZ=0 NormalX=0 NormalY=0 NormalZ=1 AngleXU=0 Radius=1
  constraints (18):
    c: Coincident(g0,g1)
    c: Coincident(g1,g2)
    c: Coincident(g2,g3)
    c: Coincident(g3,g4)
    c: Coincident(g4,g5)
    c: Coincident(g5,g0)
    c: Equal(g0, g1-g5) x5
    c: PointOnObject(g0,g6)
    c: PointOnObject(g1,g6)
    c: PointOnObject(g2,g6)
    c: PointOnObject(g3,g6)
    c: PointOnObject(g4,g6)
    c: PointOnObject(g5,g6)
    c: Coincident(g6,g-1)
    c: PointOnObject(g5,g-2)
    c: DistanceX(g0,g4) = 4
    c: Coincident(g7,g-1)
    c: Radius(g7) = 1
FEATURE [PartDesign::Pad] Pad907  label="M3 Nut Primitive181"
  Length = 0.6
  Length2 = 0.6
  Profile = -> Sketch2063
  Type = 4
FEATURE [Sketcher::SketchObject] Sketch2058
  ExternalGeometry = -> [Pad907]
  MapMode = 5
  Placement = pos=(0,0,0) rot=(0.57735,0.57735,0.57735;2.0944rad)
  Support = -> [YZ_Plane815]
  sketch-geometry (6):
    g0: LineSegment StartX=-1.9594 StartY=0.6 StartZ=0 EndX=-2.8094 EndY=0.6 EndZ=0
    g1: LineSegment StartX=-2.8094 StartY=0.6 StartZ=0 EndX=-2.8094 EndY=-0.6 EndZ=0
    g2: LineSegment StartX=-2.8094 StartY=-0.6 StartZ=0 EndX=-1.9594 EndY=-0.6 EndZ=0
    g3: LineSegment StartX=-1.9594 StartY=-0.6 StartZ=0 EndX=-2.3094 EndY=-0.4 EndZ=0
    g4: LineSegment StartX=-2.3094 StartY=-0.4 StartZ=0 EndX=-2.3094 EndY=0.4 EndZ=0
    g5: LineSegment StartX=-2.3094 StartY=0.4 StartZ=0 EndX=-1.9594 EndY=0.6 EndZ=0
  constraints (15):
    c: Horizontal(g0)
    c: Coincident(g0,g1)
    c: Coincident(g1,g2)
    c: Coincident(g2,g3)
    c: Coincident(g3,g4)
    c: Coincident(g4,g5)
    c: Coincident(g5,g0)
    c: Symmetric(g4,g3,g-1)
    c: Symmetric(g0,g2,g-1)
    c: Symmetric(g1,g0,g-1)
    c: DistanceX(g0,g4) = 0.5
    c: DistanceY(g3,g4) = 0.8
    c: DistanceY(g1,g0) = 1.2
    c: PointOnObject(g3,g-3)
    c: DistanceX(g4,g0) = 0.35
FEATURE [PartDesign::Groove] Groove189  label="M3 Nut Smooth181"
  Angle = 360
  Axis = (-2e-16,3e-16,1)
  Base = (0,0,0)
  BaseFeature = -> Pad907
  Profile = -> Sketch2058
  ReferenceAxis = -> Sketch2058 [V_Axis]
  Reversed = true
FEATURE [PartDesign::Chamfer] Chamfer431  label="M3 Nut Smooth Hole182"
  Base = -> Groove189 [Edge24,Edge23]
  BaseFeature = -> Groove189
  Size = 0.2
FEATURE [PartDesign::Body] Body576  label="M2 Nut071"
  Group = -> [Sketch2063,Pad907,Sketch2058,Groove189,Chamfer431,Sketch2061,Sketch2056]
  Origin = -> Origin810
  Placement = pos=(0,0,2.75) rot=(0,0,1;0rad)
  Tip = -> Chamfer431
FEATURE [Sketcher::SketchObject] Sketch2064
  MapMode = 5
  Support = -> [XY_Plane806]
FEATURE [Sketcher::SketchObject] Sketch2065
  MapMode = 5
  Support = -> [XY_Plane805]
FEATURE [Sketcher::SketchObject] Sketch2066
  MapMode = 5
  Support = -> [XY_Plane819]
  sketch-geometry (8):
    g0: LineSegment StartX=0 StartY=2.3094 StartZ=0 EndX=-2 EndY=1.1547 EndZ=0
    g1: LineSegment StartX=-2 StartY=1.1547 StartZ=0 EndX=-2 EndY=-1.1547 EndZ=0
    g2: LineSegment StartX=-2 StartY=-1.1547 StartZ=0 EndX=-2e-16 EndY=-2.3094 EndZ=0
    g3: LineSegment StartX=-2e-16 StartY=-2.3094 StartZ=0 EndX=2 EndY=-1.1547 EndZ=0
    g4: LineSegment StartX=2 StartY=-1.1547 StartZ=0 EndX=2 EndY=1.1547 EndZ=0
    g5: LineSegment StartX=2 StartY=1.1547 StartZ=0 EndX=0 EndY=2.3094 EndZ=0
    g6: Circle [constr] CenterX=0 CenterY=0 CenterZ=0 NormalX=0 NormalY=0 NormalZ=1 AngleXU=0 Radius=2.3094
    g7: Circle CenterX=0 CenterY=0 CenterZ=0 NormalX=0 NormalY=0 NormalZ=1 AngleXU=0 Radius=1
  constraints (18):
    c: Coincident(g0,g1)
    c: Coincident(g1,g2)
    c: Coincident(g2,g3)
    c: Coincident(g3,g4)
    c: Coincident(g4,g5)
    c: Coincident(g5,g0)
    c: Equal(g0, g1-g5) x5
    c: PointOnObject(g0,g6)
    c: PointOnObject(g1,g6)
    c: PointOnObject(g2,g6)
    c: PointOnObject(g3,g6)
    c: PointOnObject(g4,g6)
    c: PointOnObject(g5,g6)
    c: Coincident(g6,g-1)
    c: PointOnObject(g5,g-2)
    c: DistanceX(g0,g4) = 4
    c: Coincident(g7,g-1)
    c: Radius(g7) = 1
FEATURE [PartDesign::Pad] Pad910  label="M3 Nut Primitive182"
  Length = 0.6
  Length2 = 0.6
  Profile = -> Sketch2066
  Type = 4
FEATURE [Sketcher::SketchObject] Sketch2067
  MapMode = 5
  Support = -> [XY_Plane806]
FEATURE [Sketcher::SketchObject] Sketch2068
  MapMode = 5
  Support = -> [XY_Plane807]
  sketch-geometry (1):
    g0: Circle CenterX=0 CenterY=0 CenterZ=0 NormalX=0 NormalY=0 NormalZ=1 AngleXU=0 Radius=1.9
  constraints (2):
    c: Coincident(g0,g-1)
    c: Radius(g0) = 1.9
FEATURE [PartDesign::Pad] Pad908  label="M3x8 Head115"
  Length = 2
  Length2 = 100
  Profile = -> Sketch2068
  Type = 0
FEATURE [Sketcher::SketchObject] Sketch2069
  MapMode = 5
  Support = -> [XY_Plane805]
FEATURE [Sketcher::SketchObject] Sketch2070
  ExternalGeometry = -> [Pad906]
  MapMode = 5
  Placement = pos=(0,0,0) rot=(0.57735,0.57735,0.57735;2.0944rad)
  Support = -> [YZ_Plane797]
  sketch-geometry (6):
    g0: LineSegment StartX=-1.9594 StartY=0.6 StartZ=0 EndX=-2.8094 EndY=0.6 EndZ=0
    g1: LineSegment StartX=-2.8094 StartY=0.6 StartZ=0 EndX=-2.8094 EndY=-0.6 EndZ=0
    g2: LineSegment StartX=-2.8094 StartY=-0.6 StartZ=0 EndX=-1.9594 EndY=-0.6 EndZ=0
    g3: LineSegment StartX=-1.9594 StartY=-0.6 StartZ=0 EndX=-2.3094 EndY=-0.4 EndZ=0
    g4: LineSegment StartX=-2.3094 StartY=-0.4 StartZ=0 EndX=-2.3094 EndY=0.4 EndZ=0
    g5: LineSegment StartX=-2.3094 StartY=0.4 StartZ=0 EndX=-1.9594 EndY=0.6 EndZ=0
  constraints (15):
    c: Horizontal(g0)
    c: Coincident(g0,g1)
    c: Coincident(g1,g2)
    c: Coincident(g2,g3)
    c: Coincident(g3,g4)
    c: Coincident(g4,g5)
    c: Coincident(g5,g0)
    c: Symmetric(g4,g3,g-1)
    c: Symmetric(g0,g2,g-1)
    c: Symmetric(g1,g0,g-1)
    c: DistanceX(g0,g4) = 0.5
    c: DistanceY(g3,g4) = 0.8
    c: DistanceY(g1,g0) = 1.2
    c: PointOnObject(g3,g-3)
    c: DistanceX(g4,g0) = 0.35
FEATURE [PartDesign::Groove] Groove188  label="M3 Nut Smooth180"
  Angle = 360
  Axis = (-2e-16,3e-16,1)
  Base = (0,0,0)
  BaseFeature = -> Pad906
  Profile = -> Sketch2070
  ReferenceAxis = -> Sketch2070 [V_Axis]
  Reversed = true
FEATURE [PartDesign::Chamfer] Chamfer429  label="M3 Nut Smooth Hole181"
  Base = -> Groove188 [Edge24,Edge23]
  BaseFeature = -> Groove188
  Size = 0.2
FEATURE [PartDesign::Body] Body578  label="M2 Nut072"
  Group = -> [Sketch2062,Pad906,Sketch2070,Groove188,Chamfer429,Sketch2067,Sketch2064]
  Origin = -> Origin813
  Placement = pos=(0,0,2.75) rot=(0,0,1;0rad)
  Tip = -> Chamfer429
FEATURE [Sketcher::SketchObject] Sketch2072
  MapMode = 5
  Support = -> [XY_Plane821]
  sketch-geometry (1):
    g0: Circle CenterX=0 CenterY=0 CenterZ=0 NormalX=0 NormalY=0 NormalZ=1 AngleXU=0 Radius=1.9
  constraints (2):
    c: Coincident(g0,g-1)
    c: Radius(g0) = 1.9
FEATURE [PartDesign::Pad] Pad905  label="M3x8 Head114"
  Length = 2
  Length2 = 100
  Profile = -> Sketch2072
  Type = 0
FEATURE [PartDesign::Chamfer] Chamfer433  label="M3x8 Smooth116"
  Base = -> Pocket750 [Face11,Edge2,Edge24,Edge3]
  BaseFeature = -> Pocket750
  Size = 0.2
FEATURE [PartDesign::Body] Body573  label="M2x081"
  Group = -> [Sketch2057,Pad911,Sketch2059,Pad912,Sketch2060,Pocket750,Chamfer433]
  Origin = -> Origin809
  Tip = -> Chamfer433
FEATURE [App::Part] Part231  label="M071"
  Group = -> [Body573,Body576]
  Origin = -> Origin820
  Placement = pos=(-9.8e-15,10.5,80) rot=(0,1,0;3.14159rad)
FEATURE [Sketcher::SketchObject] Sketch2074
  MapMode = 5
  Support = -> [XY_Plane815]
  sketch-geometry (8):
    g0: LineSegment StartX=0 StartY=2.3094 StartZ=0 EndX=-2 EndY=1.1547 EndZ=0
    g1: LineSegment StartX=-2 StartY=1.1547 StartZ=0 EndX=-2 EndY=-1.1547 EndZ=0
    g2: LineSegment StartX=-2 StartY=-1.1547 StartZ=0 EndX=-2e-16 EndY=-2.3094 EndZ=0
    g3: LineSegment StartX=-2e-16 StartY=-2.3094 StartZ=0 EndX=2 EndY=-1.1547 EndZ=0
    g4: LineSegment StartX=2 StartY=-1.1547 StartZ=0 EndX=2 EndY=1.1547 EndZ=0
    g5: LineSegment StartX=2 StartY=1.1547 StartZ=0 EndX=0 EndY=2.3094 EndZ=0
    g6: Circle [constr] CenterX=0 CenterY=0 CenterZ=0 NormalX=0 NormalY=0 NormalZ=1 AngleXU=0 Radius=2.3094
    g7: Circle CenterX=0 CenterY=0 CenterZ=0 NormalX=0 NormalY=0 NormalZ=1 AngleXU=0 Radius=1
  constraints (18):
    c: Coincident(g0,g1)
    c: Coincident(g1,g2)
    c: Coincident(g2,g3)
    c: Coincident(g3,g4)
    c: Coincident(g4,g5)
    c: Coincident(g5,g0)
    c: Equal(g0, g1-g5) x5
    c: PointOnObject(g0,g6)
    c: PointOnObject(g1,g6)
    c: PointOnObject(g2,g6)
    c: PointOnObject(g3,g6)
    c: PointOnObject(g4,g6)
    c: PointOnObject(g5,g6)
    c: Coincident(g6,g-1)
    c: PointOnObject(g5,g-2)
    c: DistanceX(g0,g4) = 4
    c: Coincident(g7,g-1)
    c: Radius(g7) = 1
FEATURE [PartDesign::Pad] Pad915  label="M3 Nut Primitive183"
  Length = 0.6
  Length2 = 0.6
  Profile = -> Sketch2074
  Type = 4
FEATURE [Sketcher::SketchObject] Sketch2075
  MapMode = 5
  Support = -> [XY_Plane814]
  sketch-geometry (1):
    g0: Circle CenterX=0 CenterY=0 CenterZ=0 NormalX=0 NormalY=0 NormalZ=1 AngleXU=0 Radius=1.9
  constraints (2):
    c: Coincident(g0,g-1)
    c: Radius(g0) = 1.9
FEATURE [PartDesign::Pad] Pad901  label="M3x8 Head113"
  Length = 2
  Length2 = 100
  Profile = -> Sketch2075
  Type = 0
FEATURE [Sketcher::SketchObject] Sketch2073
  MapMode = 5
  Placement = pos=(0,0,2) rot=(0,0,1;0rad)
  Support = -> [Pad901]
  sketch-geometry (1):
    g0: Circle CenterX=0 CenterY=0 CenterZ=0 NormalX=0 NormalY=0 NormalZ=1 AngleXU=0 Radius=1
  constraints (2):
    c: Coincident(g0,g-1)
    c: Radius(g0) = 1
FEATURE [PartDesign::Pad] Pad902  label="M3x8 Thread113"
  BaseFeature = -> Pad901
  Length = 8
  Length2 = 100
  Profile = -> Sketch2073
  Type = 0
FEATURE [Sketcher::SketchObject] Sketch2077
  MapMode = 5
  Support = -> [XY_Plane810]
  sketch-geometry (1):
    g0: Circle CenterX=0 CenterY=0 CenterZ=0 NormalX=0 NormalY=0 NormalZ=1 AngleXU=0 Radius=1.9
  constraints (2):
    c: Coincident(g0,g-1)
    c: Radius(g0) = 1.9
FEATURE [PartDesign::Pad] Pad914  label="M3x8 Head117"
  Length = 2
  Length2 = 100
  Profile = -> Sketch2077
  Type = 0
FEATURE [Sketcher::SketchObject] Sketch2078
  MapMode = 5
  Placement = pos=(0,0,0) rot=(1,0,0;3.14159rad)
  Support = -> [Pad902]
  sketch-geometry (7):
    g0: LineSegment StartX=0.77 StartY=0.44456 StartZ=0 EndX=0 EndY=0.889119 EndZ=0
    g1: LineSegment StartX=0 StartY=0.889119 StartZ=0 EndX=-0.77 EndY=0.44456 EndZ=0
    g2: LineSegment StartX=-0.77 StartY=0.44456 StartZ=0 EndX=-0.77 EndY=-0.44456 EndZ=0
    g3: LineSegment StartX=-0.77 StartY=-0.44456 StartZ=0 EndX=3.85628e-11 EndY=-0.889119 EndZ=0
    g4: LineSegment StartX=3.85628e-11 StartY=-0.889119 StartZ=0 EndX=0.77 EndY=-0.44456 EndZ=0
    g5: LineSegment StartX=0.77 StartY=-0.44456 StartZ=0 EndX=0.77 EndY=0.44456 EndZ=0
    g6: Circle [constr] CenterX=0 CenterY=0 CenterZ=0 NormalX=0 NormalY=0 NormalZ=1 AngleXU=0 Radius=0.889119
  constraints (16):
    c: Coincident(g0,g1)
    c: Coincident(g1,g2)
    c: Coincident(g2,g3)
    c: Coincident(g3,g4)
    c: Coincident(g4,g5)
    c: Coincident(g5,g0)
    c: Equal(g0, g1-g5) x5
    c: PointOnObject(g0,g6)
    c: PointOnObject(g1,g6)
    c: PointOnObject(g2,g6)
    c: PointOnObject(g3,g6)
    c: PointOnObject(g4,g6)
    c: PointOnObject(g5,g6)
    c: Coincident(g6,g-1)
    c: PointOnObject(g0,g-2)
    c: DistanceX(g1,g0) = 1.54
FEATURE [PartDesign::Pocket] Pocket749  label="M3x8 Wrench113"
  BaseFeature = -> Pad902
  Length = 1
  Length2 = 100
  Profile = -> Sketch2078
  Type = 0
FEATURE [PartDesign::Chamfer] Chamfer424  label="M3x8 Smooth112"
  Base = -> Pocket749 [Face11,Edge2,Edge24,Edge3]
  BaseFeature = -> Pocket749
  Size = 0.2
FEATURE [PartDesign::Body] Body582  label="M2x085"
  Group = -> [Sketch2075,Pad901,Sketch2073,Pad902,Sketch2078,Pocket749,Chamfer424]
  Origin = -> Origin817
  Tip = -> Chamfer424
FEATURE [Sketcher::SketchObject] Sketch2080
  MapMode = 5
  Placement = pos=(0,0,2) rot=(0,0,1;0rad)
  Support = -> [Pad908]
  sketch-geometry (1):
    g0: Circle CenterX=0 CenterY=0 CenterZ=0 NormalX=0 NormalY=0 NormalZ=1 AngleXU=0 Radius=1
  constraints (2):
    c: Coincident(g0,g-1)
    c: Radius(g0) = 1
FEATURE [PartDesign::Pad] Pad903  label="M3x8 Thread114"
  BaseFeature = -> Pad908
  Length = 8
  Length2 = 100
  Profile = -> Sketch2080
  Type = 0
FEATURE [Sketcher::SketchObject] Sketch2079
  MapMode = 5
  Placement = pos=(0,0,0) rot=(1,0,0;3.14159rad)
  Support = -> [Pad903]
  sketch-geometry (7):
    g0: LineSegment StartX=0.77 StartY=0.44456 StartZ=0 EndX=0 EndY=0.889119 EndZ=0
    g1: LineSegment StartX=0 StartY=0.889119 StartZ=0 EndX=-0.77 EndY=0.44456 EndZ=0
    g2: LineSegment StartX=-0.77 StartY=0.44456 StartZ=0 EndX=-0.77 EndY=-0.44456 EndZ=0
    g3: LineSegment StartX=-0.77 StartY=-0.44456 StartZ=0 EndX=3.85628e-11 EndY=-0.889119 EndZ=0
    g4: LineSegment StartX=3.85628e-11 StartY=-0.889119 StartZ=0 EndX=0.77 EndY=-0.44456 EndZ=0
    g5: LineSegment StartX=0.77 StartY=-0.44456 StartZ=0 EndX=0.77 EndY=0.44456 EndZ=0
    g6: Circle [constr] CenterX=0 CenterY=0 CenterZ=0 NormalX=0 NormalY=0 NormalZ=1 AngleXU=0 Radius=0.889119
  constraints (16):
    c: Coincident(g0,g1)
    c: Coincident(g1,g2)
    c: Coincident(g2,g3)
    c: Coincident(g3,g4)
    c: Coincident(g4,g5)
    c: Coincident(g5,g0)
    c: Equal(g0, g1-g5) x5
    c: PointOnObject(g0,g6)
    c: PointOnObject(g1,g6)
    c: PointOnObject(g2,g6)
    c: PointOnObject(g3,g6)
    c: PointOnObject(g4,g6)
    c: PointOnObject(g5,g6)
    c: Coincident(g6,g-1)
    c: PointOnObject(g0,g-2)
    c: DistanceX(g1,g0) = 1.54
FEATURE [PartDesign::Pocket] Pocket751  label="M3x8 Wrench115"
  BaseFeature = -> Pad903
  Length = 1
  Length2 = 100
  Profile = -> Sketch2079
  Type = 0
FEATURE [PartDesign::Chamfer] Chamfer435  label="M3x8 Smooth117"
  Base = -> Pocket751 [Face11,Edge2,Edge24,Edge3]
  BaseFeature = -> Pocket751
  Size = 0.2
FEATURE [PartDesign::Body] Body577  label="M2x083"
  Group = -> [Sketch2068,Pad908,Sketch2080,Pad903,Sketch2079,Pocket751,Chamfer435]
  Origin = -> Origin814
  Tip = -> Chamfer435
FEATURE [Sketcher::SketchObject] Sketch2081
  MapMode = 5
  Placement = pos=(0,0,2) rot=(0,0,1;0rad)
  Support = -> [Pad905]
  sketch-geometry (1):
    g0: Circle CenterX=0 CenterY=0 CenterZ=0 NormalX=0 NormalY=0 NormalZ=1 AngleXU=0 Radius=1
  constraints (2):
    c: Coincident(g0,g-1)
    c: Radius(g0) = 1
FEATURE [PartDesign::Pad] Pad909  label="M3x8 Thread115"
  BaseFeature = -> Pad905
  Length = 8
  Length2 = 100
  Profile = -> Sketch2081
  Type = 0
FEATURE [Sketcher::SketchObject] Sketch2082
  MapMode = 5
  Placement = pos=(0,0,0) rot=(1,0,0;3.14159rad)
  Support = -> [Pad909]
  sketch-geometry (7):
    g0: LineSegment StartX=0.77 StartY=0.44456 StartZ=0 EndX=0 EndY=0.889119 EndZ=0
    g1: LineSegment StartX=0 StartY=0.889119 StartZ=0 EndX=-0.77 EndY=0.44456 EndZ=0
    g2: LineSegment StartX=-0.77 StartY=0.44456 StartZ=0 EndX=-0.77 EndY=-0.44456 EndZ=0
    g3: LineSegment StartX=-0.77 StartY=-0.44456 StartZ=0 EndX=3.85628e-11 EndY=-0.889119 EndZ=0
    g4: LineSegment StartX=3.85628e-11 StartY=-0.889119 StartZ=0 EndX=0.77 EndY=-0.44456 EndZ=0
    g5: LineSegment StartX=0.77 StartY=-0.44456 StartZ=0 EndX=0.77 EndY=0.44456 EndZ=0
    g6: Circle [constr] CenterX=0 CenterY=0 CenterZ=0 NormalX=0 NormalY=0 NormalZ=1 AngleXU=0 Radius=0.889119
  constraints (16):
    c: Coincident(g0,g1)
    c: Coincident(g1,g2)
    c: Coincident(g2,g3)
    c: Coincident(g3,g4)
    c: Coincident(g4,g5)
    c: Coincident(g5,g0)
    c: Equal(g0, g1-g5) x5
    c: PointOnObject(g0,g6)
    c: PointOnObject(g1,g6)
    c: PointOnObject(g2,g6)
    c: PointOnObject(g3,g6)
    c: PointOnObject(g4,g6)
    c: PointOnObject(g5,g6)
    c: Coincident(g6,g-1)
    c: PointOnObject(g0,g-2)
    c: DistanceX(g1,g0) = 1.54
FEATURE [PartDesign::Pocket] Pocket752  label="M3x8 Wrench116"
  BaseFeature = -> Pad909
  Length = 1
  Length2 = 100
  Profile = -> Sketch2082
  Type = 0
FEATURE [PartDesign::Chamfer] Chamfer430  label="M3x8 Smooth115"
  Base = -> Pocket752 [Face11,Edge2,Edge24,Edge3]
  BaseFeature = -> Pocket752
  Size = 0.2
FEATURE [PartDesign::Body] Body574  label="M2x082"
  Group = -> [Sketch2072,Pad905,Sketch2081,Pad909,Sketch2082,Pocket752,Chamfer430]
  Origin = -> Origin812
  Tip = -> Chamfer430
FEATURE [App::Part] Part230  label="M070"
  Group = -> [Body574,Body578]
  Origin = -> Origin819
  Placement = pos=(-9.1,-5.25,80) rot=(0,1,0;3.14159rad)
FEATURE [Sketcher::SketchObject] Sketch2083
  MapMode = 5
  Support = -> [XY_Plane805]
  sketch-geometry (8):
    g0: LineSegment StartX=0 StartY=2.3094 StartZ=0 EndX=-2 EndY=1.1547 EndZ=0
    g1: LineSegment StartX=-2 StartY=1.1547 StartZ=0 EndX=-2 EndY=-1.1547 EndZ=0
    g2: LineSegment StartX=-2 StartY=-1.1547 StartZ=0 EndX=-2e-16 EndY=-2.3094 EndZ=0
    g3: LineSegment StartX=-2e-16 StartY=-2.3094 StartZ=0 EndX=2 EndY=-1.1547 EndZ=0
    g4: LineSegment StartX=2 StartY=-1.1547 StartZ=0 EndX=2 EndY=1.1547 EndZ=0
    g5: LineSegment StartX=2 StartY=1.1547 StartZ=0 EndX=0 EndY=2.3094 EndZ=0
    g6: Circle [constr] CenterX=0 CenterY=0 CenterZ=0 NormalX=0 NormalY=0 NormalZ=1 AngleXU=0 Radius=2.3094
    g7: Circle CenterX=0 CenterY=0 CenterZ=0 NormalX=0 NormalY=0 NormalZ=1 AngleXU=0 Radius=1
  constraints (18):
    c: Coincident(g0,g1)
    c: Coincident(g1,g2)
    c: Coincident(g2,g3)
    c: Coincident(g3,g4)
    c: Coincident(g4,g5)
    c: Coincident(g5,g0)
    c: Equal(g0, g1-g5) x5
    c: PointOnObject(g0,g6)
    c: PointOnObject(g1,g6)
    c: PointOnObject(g2,g6)
    c: PointOnObject(g3,g6)
    c: PointOnObject(g4,g6)
    c: PointOnObject(g5,g6)
    c: Coincident(g6,g-1)
    c: PointOnObject(g5,g-2)
    c: DistanceX(g0,g4) = 4
    c: Coincident(g7,g-1)
    c: Radius(g7) = 1
FEATURE [PartDesign::Pad] Pad904  label="M3 Nut Primitive179"
  Length = 0.6
  Length2 = 0.6
  Profile = -> Sketch2083
  Type = 4
FEATURE [Sketcher::SketchObject] Sketch2071
  ExternalGeometry = -> [Pad904]
  MapMode = 5
  Placement = pos=(0,0,0) rot=(0.57735,0.57735,0.57735;2.0944rad)
  Support = -> [YZ_Plane799]
  sketch-geometry (6):
    g0: LineSegment StartX=-1.9594 StartY=0.6 StartZ=0 EndX=-2.8094 EndY=0.6 EndZ=0
    g1: LineSegment StartX=-2.8094 StartY=0.6 StartZ=0 EndX=-2.8094 EndY=-0.6 EndZ=0
    g2: LineSegment StartX=-2.8094 StartY=-0.6 StartZ=0 EndX=-1.9594 EndY=-0.6 EndZ=0
    g3: LineSegment StartX=-1.9594 StartY=-0.6 StartZ=0 EndX=-2.3094 EndY=-0.4 EndZ=0
    g4: LineSegment StartX=-2.3094 StartY=-0.4 StartZ=0 EndX=-2.3094 EndY=0.4 EndZ=0
    g5: LineSegment StartX=-2.3094 StartY=0.4 StartZ=0 EndX=-1.9594 EndY=0.6 EndZ=0
  constraints (15):
    c: Horizontal(g0)
    c: Coincident(g0,g1)
    c: Coincident(g1,g2)
    c: Coincident(g2,g3)
    c: Coincident(g3,g4)
    c: Coincident(g4,g5)
    c: Coincident(g5,g0)
    c: Symmetric(g4,g3,g-1)
    c: Symmetric(g0,g2,g-1)
    c: Symmetric(g1,g0,g-1)
    c: DistanceX(g0,g4) = 0.5
    c: DistanceY(g3,g4) = 0.8
    c: DistanceY(g1,g0) = 1.2
    c: PointOnObject(g3,g-3)
    c: DistanceX(g4,g0) = 0.35
FEATURE [PartDesign::Groove] Groove190  label="M3 Nut Smooth182"
  Angle = 360
  Axis = (-2e-16,3e-16,1)
  Base = (0,0,0)
  BaseFeature = -> Pad904
  Profile = -> Sketch2071
  ReferenceAxis = -> Sketch2071 [V_Axis]
  Reversed = true
FEATURE [PartDesign::Chamfer] Chamfer432  label="M3 Nut Smooth Hole183"
  Base = -> Groove190 [Edge24,Edge23]
  BaseFeature = -> Groove190
  Size = 0.2
FEATURE [PartDesign::Body] Body575  label="M2 Nut070"
  Group = -> [Sketch2083,Pad904,Sketch2071,Groove190,Chamfer432,Sketch2069,Sketch2065]
  Origin = -> Origin806
  Placement = pos=(0,0,2.75) rot=(0,0,1;0rad)
  Tip = -> Chamfer432
FEATURE [App::Part] Part232  label="M072"
  Group = -> [Body577,Body575]
  Origin = -> Origin805
  Placement = pos=(-9.8e-15,-10.5,80) rot=(0,1,0;3.14159rad)
FEATURE [Sketcher::SketchObject] Sketch2084
  ExternalGeometry = -> [Pad910]
  MapMode = 5
  Placement = pos=(0,0,0) rot=(0.57735,0.57735,0.57735;2.0944rad)
  Support = -> [YZ_Plane812]
  sketch-geometry (6):
    g0: LineSegment StartX=-1.9594 StartY=0.6 StartZ=0 EndX=-2.8094 EndY=0.6 EndZ=0
    g1: LineSegment StartX=-2.8094 StartY=0.6 StartZ=0 EndX=-2.8094 EndY=-0.6 EndZ=0
    g2: LineSegment StartX=-2.8094 StartY=-0.6 StartZ=0 EndX=-1.9594 EndY=-0.6 EndZ=0
    g3: LineSegment StartX=-1.9594 StartY=-0.6 StartZ=0 EndX=-2.3094 EndY=-0.4 EndZ=0
    g4: LineSegment StartX=-2.3094 StartY=-0.4 StartZ=0 EndX=-2.3094 EndY=0.4 EndZ=0
    g5: LineSegment StartX=-2.3094 StartY=0.4 StartZ=0 EndX=-1.9594 EndY=0.6 EndZ=0
  constraints (15):
    c: Horizontal(g0)
    c: Coincident(g0,g1)
    c: Coincident(g1,g2)
    c: Coincident(g2,g3)
    c: Coincident(g3,g4)
    c: Coincident(g4,g5)
    c: Coincident(g5,g0)
    c: Symmetric(g4,g3,g-1)
    c: Symmetric(g0,g2,g-1)
    c: Symmetric(g1,g0,g-1)
    c: DistanceX(g0,g4) = 0.5
    c: DistanceY(g3,g4) = 0.8
    c: DistanceY(g1,g0) = 1.2
    c: PointOnObject(g3,g-3)
    c: DistanceX(g4,g0) = 0.35
FEATURE [PartDesign::Groove] Groove187  label="M3 Nut Smooth179"
  Angle = 360
  Axis = (-2e-16,3e-16,1)
  Base = (0,0,0)
  BaseFeature = -> Pad910
  Profile = -> Sketch2084
  ReferenceAxis = -> Sketch2084 [V_Axis]
  Reversed = true
FEATURE [PartDesign::Chamfer] Chamfer434  label="M3 Nut Smooth Hole184"
  Base = -> Groove187 [Edge24,Edge23]
  BaseFeature = -> Groove187
  Size = 0.2
FEATURE [Sketcher::SketchObject] Sketch2085
  ExternalGeometry = -> [Pad915]
  MapMode = 5
  Placement = pos=(0,0,0) rot=(0.57735,0.57735,0.57735;2.0944rad)
  Support = -> [YZ_Plane805]
  sketch-geometry (6):
    g0: LineSegment StartX=-1.9594 StartY=0.6 StartZ=0 EndX=-2.8094 EndY=0.6 EndZ=0
    g1: LineSegment StartX=-2.8094 StartY=0.6 StartZ=0 EndX=-2.8094 EndY=-0.6 EndZ=0
    g2: LineSegment StartX=-2.8094 StartY=-0.6 StartZ=0 EndX=-1.9594 EndY=-0.6 EndZ=0
    g3: LineSegment StartX=-1.9594 StartY=-0.6 StartZ=0 EndX=-2.3094 EndY=-0.4 EndZ=0
    g4: LineSegment StartX=-2.3094 StartY=-0.4 StartZ=0 EndX=-2.3094 EndY=0.4 EndZ=0
    g5: LineSegment StartX=-2.3094 StartY=0.4 StartZ=0 EndX=-1.9594 EndY=0.6 EndZ=0
  constraints (15):
    c: Horizontal(g0)
    c: Coincident(g0,g1)
    c: Coincident(g1,g2)
    c: Coincident(g2,g3)
    c: Coincident(g3,g4)
    c: Coincident(g4,g5)
    c: Coincident(g5,g0)
    c: Symmetric(g4,g3,g-1)
    c: Symmetric(g0,g2,g-1)
    c: Symmetric(g1,g0,g-1)
    c: DistanceX(g0,g4) = 0.5
    c: DistanceY(g3,g4) = 0.8
    c: DistanceY(g1,g0) = 1.2
    c: PointOnObject(g3,g-3)
    c: DistanceX(g4,g0) = 0.35
FEATURE [PartDesign::Groove] Groove191  label="M3 Nut Smooth183"
  Angle = 360
  Axis = (-2e-16,3e-16,1)
  Base = (0,0,0)
  BaseFeature = -> Pad915
  Profile = -> Sketch2085
  ReferenceAxis = -> Sketch2085 [V_Axis]
  Reversed = true
FEATURE [PartDesign::Chamfer] Chamfer425  label="M3 Nut Smooth Hole179"
  Base = -> Groove191 [Edge24,Edge23]
  BaseFeature = -> Groove191
  Size = 0.2
FEATURE [Sketcher::SketchObject] Sketch2086
  MapMode = 5
  Placement = pos=(0,0,2) rot=(0,0,1;0rad)
  Support = -> [Pad914]
  sketch-geometry (1):
    g0: Circle CenterX=0 CenterY=0 CenterZ=0 NormalX=0 NormalY=0 NormalZ=1 AngleXU=0 Radius=1
  constraints (2):
    c: Coincident(g0,g-1)
    c: Radius(g0) = 1
FEATURE [PartDesign::Pad] Pad917  label="M3x8 Thread118"
  BaseFeature = -> Pad914
  Length = 8
  Length2 = 100
  Profile = -> Sketch2086
  Type = 0
FEATURE [Sketcher::SketchObject] Sketch2087
  MapMode = 5
  Placement = pos=(0,0,0) rot=(1,0,0;3.14159rad)
  Support = -> [Pad917]
  sketch-geometry (7):
    g0: LineSegment StartX=0.77 StartY=0.44456 StartZ=0 EndX=0 EndY=0.889119 EndZ=0
    g1: LineSegment StartX=0 StartY=0.889119 StartZ=0 EndX=-0.77 EndY=0.44456 EndZ=0
    g2: LineSegment StartX=-0.77 StartY=0.44456 StartZ=0 EndX=-0.77 EndY=-0.44456 EndZ=0
    g3: LineSegment StartX=-0.77 StartY=-0.44456 StartZ=0 EndX=3.85628e-11 EndY=-0.889119 EndZ=0
    g4: LineSegment StartX=3.85628e-11 StartY=-0.889119 StartZ=0 EndX=0.77 EndY=-0.44456 EndZ=0
    g5: LineSegment StartX=0.77 StartY=-0.44456 StartZ=0 EndX=0.77 EndY=0.44456 EndZ=0
    g6: Circle [constr] CenterX=0 CenterY=0 CenterZ=0 NormalX=0 NormalY=0 NormalZ=1 AngleXU=0 Radius=0.889119
  constraints (16):
    c: Coincident(g0,g1)
    c: Coincident(g1,g2)
    c: Coincident(g2,g3)
    c: Coincident(g3,g4)
    c: Coincident(g4,g5)
    c: Coincident(g5,g0)
    c: Equal(g0, g1-g5) x5
    c: PointOnObject(g0,g6)
    c: PointOnObject(g1,g6)
    c: PointOnObject(g2,g6)
    c: PointOnObject(g3,g6)
    c: PointOnObject(g4,g6)
    c: PointOnObject(g5,g6)
    c: Coincident(g6,g-1)
    c: PointOnObject(g0,g-2)
    c: DistanceX(g1,g0) = 1.54
FEATURE [PartDesign::Pocket] Pocket754  label="M3x8 Wrench118"
  BaseFeature = -> Pad917
  Length = 1
  Length2 = 100
  Profile = -> Sketch2087
  Type = 0
FEATURE [PartDesign::Chamfer] Chamfer427  label="M3x8 Smooth113"
  Base = -> Pocket754 [Face11,Edge2,Edge24,Edge3]
  BaseFeature = -> Pocket754
  Size = 0.2
FEATURE [Sketcher::SketchObject] Sketch2088
  MapMode = 5
  Support = -> [XY_Plane819]
FEATURE [Sketcher::SketchObject] Sketch2089
  MapMode = 5
  Support = -> [XY_Plane815]
FEATURE [Sketcher::SketchObject] Sketch2090
  MapMode = 5
  Support = -> [XY_Plane812]
  sketch-geometry (8):
    g0: LineSegment StartX=0 StartY=2.3094 StartZ=0 EndX=-2 EndY=1.1547 EndZ=0
    g1: LineSegment StartX=-2 StartY=1.1547 StartZ=0 EndX=-2 EndY=-1.1547 EndZ=0
    g2: LineSegment StartX=-2 StartY=-1.1547 StartZ=0 EndX=-2e-16 EndY=-2.3094 EndZ=0
    g3: LineSegment StartX=-2e-16 StartY=-2.3094 StartZ=0 EndX=2 EndY=-1.1547 EndZ=0
    g4: LineSegment StartX=2 StartY=-1.1547 StartZ=0 EndX=2 EndY=1.1547 EndZ=0
    g5: LineSegment StartX=2 StartY=1.1547 StartZ=0 EndX=0 EndY=2.3094 EndZ=0
    g6: Circle [constr] CenterX=0 CenterY=0 CenterZ=0 NormalX=0 NormalY=0 NormalZ=1 AngleXU=0 Radius=2.3094
    g7: Circle CenterX=0 CenterY=0 CenterZ=0 NormalX=0 NormalY=0 NormalZ=1 AngleXU=0 Radius=1
  constraints (18):
    c: Coincident(g0,g1)
    c: Coincident(g1,g2)
    c: Coincident(g2,g3)
    c: Coincident(g3,g4)
    c: Coincident(g4,g5)
    c: Coincident(g5,g0)
    c: Equal(g0, g1-g5) x5
    c: PointOnObject(g0,g6)
    c: PointOnObject(g1,g6)
    c: PointOnObject(g2,g6)
    c: PointOnObject(g3,g6)
    c: PointOnObject(g4,g6)
    c: PointOnObject(g5,g6)
    c: Coincident(g6,g-1)
    c: PointOnObject(g5,g-2)
    c: DistanceX(g0,g4) = 4
    c: Coincident(g7,g-1)
    c: Radius(g7) = 1
FEATURE [PartDesign::Pad] Pad918  label="M3 Nut Primitive184"
  Length = 0.6
  Length2 = 0.6
  Profile = -> Sketch2090
  Type = 4
FEATURE [Sketcher::SketchObject] Sketch2091
  MapMode = 5
  Support = -> [XY_Plane815]
FEATURE [Sketcher::SketchObject] Sketch2093
  MapMode = 5
  Support = -> [XY_Plane819]
FEATURE [PartDesign::Body] Body581  label="M2 Nut074"
  Group = -> [Sketch2066,Pad910,Sketch2084,Groove187,Chamfer434,Sketch2093,Sketch2088]
  Origin = -> Origin815
  Placement = pos=(0,0,2.75) rot=(0,0,1;0rad)
  Tip = -> Chamfer434
FEATURE [App::Part] Part229  label="M069"
  Group = -> [Body582,Body581]
  Origin = -> Origin811
  Placement = pos=(9.1,-5.25,80) rot=(0,1,0;3.14159rad)
FEATURE [Sketcher::SketchObject] Sketch2094
  MapMode = 5
  Support = -> [XY_Plane813]
  sketch-geometry (1):
    g0: Circle CenterX=0 CenterY=0 CenterZ=0 NormalX=0 NormalY=0 NormalZ=1 AngleXU=0 Radius=1.9
  constraints (2):
    c: Coincident(g0,g-1)
    c: Radius(g0) = 1.9
FEATURE [PartDesign::Pad] Pad916  label="M3x8 Head118"
  Length = 2
  Length2 = 100
  Profile = -> Sketch2094
  Type = 0
FEATURE [Sketcher::SketchObject] Sketch2092
  MapMode = 5
  Placement = pos=(0,0,2) rot=(0,0,1;0rad)
  Support = -> [Pad916]
  sketch-geometry (1):
    g0: Circle CenterX=0 CenterY=0 CenterZ=0 NormalX=0 NormalY=0 NormalZ=1 AngleXU=0 Radius=1
  constraints (2):
    c: Coincident(g0,g-1)
    c: Radius(g0) = 1
FEATURE [PartDesign::Pad] Pad913  label="M3x8 Thread117"
  BaseFeature = -> Pad916
  Length = 8
  Length2 = 100
  Profile = -> Sketch2092
  Type = 0
FEATURE [Sketcher::SketchObject] Sketch2076
  MapMode = 5
  Placement = pos=(0,0,0) rot=(1,0,0;3.14159rad)
  Support = -> [Pad913]
  sketch-geometry (7):
    g0: LineSegment StartX=0.77 StartY=0.44456 StartZ=0 EndX=0 EndY=0.889119 EndZ=0
    g1: LineSegment StartX=0 StartY=0.889119 StartZ=0 EndX=-0.77 EndY=0.44456 EndZ=0
    g2: LineSegment StartX=-0.77 StartY=0.44456 StartZ=0 EndX=-0.77 EndY=-0.44456 EndZ=0
    g3: LineSegment StartX=-0.77 StartY=-0.44456 StartZ=0 EndX=3.85628e-11 EndY=-0.889119 EndZ=0
    g4: LineSegment StartX=3.85628e-11 StartY=-0.889119 StartZ=0 EndX=0.77 EndY=-0.44456 EndZ=0
    g5: LineSegment StartX=0.77 StartY=-0.44456 StartZ=0 EndX=0.77 EndY=0.44456 EndZ=0
    g6: Circle [constr] CenterX=0 CenterY=0 CenterZ=0 NormalX=0 NormalY=0 NormalZ=1 AngleXU=0 Radius=0.889119
  constraints (16):
    c: Coincident(g0,g1)
    c: Coincident(g1,g2)
    c: Coincident(g2,g3)
    c: Coincident(g3,g4)
    c: Coincident(g4,g5)
    c: Coincident(g5,g0)
    c: Equal(g0, g1-g5) x5
    c: PointOnObject(g0,g6)
    c: PointOnObject(g1,g6)
    c: PointOnObject(g2,g6)
    c: PointOnObject(g3,g6)
    c: PointOnObject(g4,g6)
    c: PointOnObject(g5,g6)
    c: Coincident(g6,g-1)
    c: PointOnObject(g0,g-2)
    c: DistanceX(g1,g0) = 1.54
FEATURE [PartDesign::Pocket] Pocket753  label="M3x8 Wrench117"
  BaseFeature = -> Pad913
  Length = 1
  Length2 = 100
  Profile = -> Sketch2076
  Type = 0
FEATURE [PartDesign::Chamfer] Chamfer428  label="M3x8 Smooth114"
  Base = -> Pocket753 [Face11,Edge2,Edge24,Edge3]
  BaseFeature = -> Pocket753
  Size = 0.2
FEATURE [PartDesign::Body] Body580  label="M2x084"
  Group = -> [Sketch2094,Pad916,Sketch2092,Pad913,Sketch2076,Pocket753,Chamfer428]
  Origin = -> Origin822
  Tip = -> Chamfer428
FEATURE [Sketcher::SketchObject] Sketch2095
  MapMode = 5
  Support = -> [XY_Plane812]
FEATURE [Sketcher::SketchObject] Sketch2096
  ExternalGeometry = -> [Pad918]
  MapMode = 5
  Placement = pos=(0,0,0) rot=(0.57735,0.57735,0.57735;2.0944rad)
  Support = -> [YZ_Plane802]
  sketch-geometry (6):
    g0: LineSegment StartX=-1.9594 StartY=0.6 StartZ=0 EndX=-2.8094 EndY=0.6 EndZ=0
    g1: LineSegment StartX=-2.8094 StartY=0.6 StartZ=0 EndX=-2.8094 EndY=-0.6 EndZ=0
    g2: LineSegment StartX=-2.8094 StartY=-0.6 StartZ=0 EndX=-1.9594 EndY=-0.6 EndZ=0
    g3: LineSegment StartX=-1.9594 StartY=-0.6 StartZ=0 EndX=-2.3094 EndY=-0.4 EndZ=0
    g4: LineSegment StartX=-2.3094 StartY=-0.4 StartZ=0 EndX=-2.3094 EndY=0.4 EndZ=0
    g5: LineSegment StartX=-2.3094 StartY=0.4 StartZ=0 EndX=-1.9594 EndY=0.6 EndZ=0
  constraints (15):
    c: Horizontal(g0)
    c: Coincident(g0,g1)
    c: Coincident(g1,g2)
    c: Coincident(g2,g3)
    c: Coincident(g3,g4)
    c: Coincident(g4,g5)
    c: Coincident(g5,g0)
    c: Symmetric(g4,g3,g-1)
    c: Symmetric(g0,g2,g-1)
    c: Symmetric(g1,g0,g-1)
    c: DistanceX(g0,g4) = 0.5
    c: DistanceY(g3,g4) = 0.8
    c: DistanceY(g1,g0) = 1.2
    c: PointOnObject(g3,g-3)
    c: DistanceX(g4,g0) = 0.35
FEATURE [PartDesign::Groove] Groove192  label="M3 Nut Smooth184"
  Angle = 360
  Axis = (-2e-16,3e-16,1)
  Base = (0,0,0)
  BaseFeature = -> Pad918
  Profile = -> Sketch2096
  ReferenceAxis = -> Sketch2096 [V_Axis]
  Reversed = true
FEATURE [PartDesign::Chamfer] Chamfer426  label="M3 Nut Smooth Hole180"
  Base = -> Groove192 [Edge24,Edge23]
  BaseFeature = -> Groove192
  Size = 0.2
FEATURE [PartDesign::Body] Body583  label="M2 Nut075"
  Group = -> [Sketch2074,Pad915,Sketch2085,Groove191,Chamfer425,Sketch2089,Sketch2091]
  Origin = -> Origin816
  Placement = pos=(0,0,2.75) rot=(0,0,1;0rad)
  Tip = -> Chamfer425
FEATURE [PartDesign::Body] Body584  label="M2x086"
  Group = -> [Sketch2077,Pad914,Sketch2086,Pad917,Sketch2087,Pocket754,Chamfer427]
  Origin = -> Origin808
  Tip = -> Chamfer427
FEATURE [App::Part] Part227  label="M068"
  Group = -> [Body584,Body583]
  Origin = -> Origin807
  Placement = pos=(9.1,5.25,80) rot=(0,1,0;3.14159rad)
FEATURE [Sketcher::SketchObject] Sketch2097
  MapMode = 5
  Support = -> [XY_Plane812]
FEATURE [PartDesign::Body] Body579  label="M2 Nut073"
  Group = -> [Sketch2090,Pad918,Sketch2096,Groove192,Chamfer426,Sketch2097,Sketch2095]
  Origin = -> Origin821
  Placement = pos=(0,0,2.75) rot=(0,0,1;0rad)
  Tip = -> Chamfer426
FEATURE [App::Part] Part233  label="M073"
  Group = -> [Body580,Body579]
  Origin = -> Origin823
  Placement = pos=(-9.1,5.25,80) rot=(0,1,0;3.14159rad)
FEATURE [App::Part] Part228  label="Screws015"
  Group = -> [Part231,Part232,Part230,Part229,Part227,Part233]
  Origin = -> Origin818
  Placement = pos=(0,0,-141) rot=(0,0,1;0rad)
FEATURE [Sketcher::SketchObject] Sketch2099
  MapMode = 5
  Support = -> [XY_Plane842]
FEATURE [Sketcher::SketchObject] Sketch2100
  MapMode = 5
  Support = -> [XY_Plane842]
FEATURE [Sketcher::SketchObject] Sketch2102
  MapMode = 5
  Support = -> [XY_Plane839]
  sketch-geometry (1):
    g0: Circle CenterX=0 CenterY=0 CenterZ=0 NormalX=0 NormalY=0 NormalZ=1 AngleXU=0 Radius=1.9
  constraints (2):
    c: Coincident(g0,g-1)
    c: Radius(g0) = 1.9
FEATURE [Sketcher::SketchObject] Sketch2104
  MapMode = 5
  Support = -> [XY_Plane827]
  sketch-geometry (8):
    g0: LineSegment StartX=0 StartY=2.3094 StartZ=0 EndX=-2 EndY=1.1547 EndZ=0
    g1: LineSegment StartX=-2 StartY=1.1547 StartZ=0 EndX=-2 EndY=-1.1547 EndZ=0
    g2: LineSegment StartX=-2 StartY=-1.1547 StartZ=0 EndX=-2e-16 EndY=-2.3094 EndZ=0
    g3: LineSegment StartX=-2e-16 StartY=-2.3094 StartZ=0 EndX=2 EndY=-1.1547 EndZ=0
    g4: LineSegment StartX=2 StartY=-1.1547 StartZ=0 EndX=2 EndY=1.1547 EndZ=0
    g5: LineSegment StartX=2 StartY=1.1547 StartZ=0 EndX=0 EndY=2.3094 EndZ=0
    g6: Circle [constr] CenterX=0 CenterY=0 CenterZ=0 NormalX=0 NormalY=0 NormalZ=1 AngleXU=0 Radius=2.3094
    g7: Circle CenterX=0 CenterY=0 CenterZ=0 NormalX=0 NormalY=0 NormalZ=1 AngleXU=0 Radius=1
  constraints (18):
    c: Coincident(g0,g1)
    c: Coincident(g1,g2)
    c: Coincident(g2,g3)
    c: Coincident(g3,g4)
    c: Coincident(g4,g5)
    c: Coincident(g5,g0)
    c: Equal(g0, g1-g5) x5
    c: PointOnObject(g0,g6)
    c: PointOnObject(g1,g6)
    c: PointOnObject(g2,g6)
    c: PointOnObject(g3,g6)
    c: PointOnObject(g4,g6)
    c: PointOnObject(g5,g6)
    c: Coincident(g6,g-1)
    c: PointOnObject(g5,g-2)
    c: DistanceX(g0,g4) = 4
    c: Coincident(g7,g-1)
    c: Radius(g7) = 1
FEATURE [Sketcher::SketchObject] Sketch2105
  MapMode = 5
  Support = -> [XY_Plane842]
  sketch-geometry (8):
    g0: LineSegment StartX=0 StartY=2.3094 StartZ=0 EndX=-2 EndY=1.1547 EndZ=0
    g1: LineSegment StartX=-2 StartY=1.1547 StartZ=0 EndX=-2 EndY=-1.1547 EndZ=0
    g2: LineSegment StartX=-2 StartY=-1.1547 StartZ=0 EndX=-2e-16 EndY=-2.3094 EndZ=0
    g3: LineSegment StartX=-2e-16 StartY=-2.3094 StartZ=0 EndX=2 EndY=-1.1547 EndZ=0
    g4: LineSegment StartX=2 StartY=-1.1547 StartZ=0 EndX=2 EndY=1.1547 EndZ=0
    g5: LineSegment StartX=2 StartY=1.1547 StartZ=0 EndX=0 EndY=2.3094 EndZ=0
    g6: Circle [constr] CenterX=0 CenterY=0 CenterZ=0 NormalX=0 NormalY=0 NormalZ=1 AngleXU=0 Radius=2.3094
    g7: Circle CenterX=0 CenterY=0 CenterZ=0 NormalX=0 NormalY=0 NormalZ=1 AngleXU=0 Radius=1
  constraints (18):
    c: Coincident(g0,g1)
    c: Coincident(g1,g2)
    c: Coincident(g2,g3)
    c: Coincident(g3,g4)
    c: Coincident(g4,g5)
    c: Coincident(g5,g0)
    c: Equal(g0, g1-g5) x5
    c: PointOnObject(g0,g6)
    c: PointOnObject(g1,g6)
    c: PointOnObject(g2,g6)
    c: PointOnObject(g3,g6)
    c: PointOnObject(g4,g6)
    c: PointOnObject(g5,g6)
    c: Coincident(g6,g-1)
    c: PointOnObject(g5,g-2)
    c: DistanceX(g0,g4) = 4
    c: Coincident(g7,g-1)
    c: Radius(g7) = 1
FEATURE [Sketcher::SketchObject] Sketch2106
  MapMode = 5
  Support = -> [XY_Plane827]
FEATURE [Sketcher::SketchObject] Sketch2107
  MapMode = 5
  Support = -> [XY_Plane825]
  sketch-geometry (1):
    g0: Circle CenterX=0 CenterY=0 CenterZ=0 NormalX=0 NormalY=0 NormalZ=1 AngleXU=0 Radius=1.9
  constraints (2):
    c: Coincident(g0,g-1)
    c: Radius(g0) = 1.9
FEATURE [Sketcher::SketchObject] Sketch2108
  MapMode = 5
  Support = -> [XY_Plane843]
  sketch-geometry (1):
    g0: Circle CenterX=0 CenterY=0 CenterZ=0 NormalX=0 NormalY=0 NormalZ=1 AngleXU=0 Radius=1.9
  constraints (2):
    c: Coincident(g0,g-1)
    c: Radius(g0) = 1.9
FEATURE [Sketcher::SketchObject] Sketch2109
  MapMode = 5
  Support = -> [XY_Plane838]
  sketch-geometry (8):
    g0: LineSegment StartX=0 StartY=2.3094 StartZ=0 EndX=-2 EndY=1.1547 EndZ=0
    g1: LineSegment StartX=-2 StartY=1.1547 StartZ=0 EndX=-2 EndY=-1.1547 EndZ=0
    g2: LineSegment StartX=-2 StartY=-1.1547 StartZ=0 EndX=-2e-16 EndY=-2.3094 EndZ=0
    g3: LineSegment StartX=-2e-16 StartY=-2.3094 StartZ=0 EndX=2 EndY=-1.1547 EndZ=0
    g4: LineSegment StartX=2 StartY=-1.1547 StartZ=0 EndX=2 EndY=1.1547 EndZ=0
    g5: LineSegment StartX=2 StartY=1.1547 StartZ=0 EndX=0 EndY=2.3094 EndZ=0
    g6: Circle [constr] CenterX=0 CenterY=0 CenterZ=0 NormalX=0 NormalY=0 NormalZ=1 AngleXU=0 Radius=2.3094
    g7: Circle CenterX=0 CenterY=0 CenterZ=0 NormalX=0 NormalY=0 NormalZ=1 AngleXU=0 Radius=1
  constraints (18):
    c: Coincident(g0,g1)
    c: Coincident(g1,g2)
    c: Coincident(g2,g3)
    c: Coincident(g3,g4)
    c: Coincident(g4,g5)
    c: Coincident(g5,g0)
    c: Equal(g0, g1-g5) x5
    c: PointOnObject(g0,g6)
    c: PointOnObject(g1,g6)
    c: PointOnObject(g2,g6)
    c: PointOnObject(g3,g6)
    c: PointOnObject(g4,g6)
    c: PointOnObject(g5,g6)
    c: Coincident(g6,g-1)
    c: PointOnObject(g5,g-2)
    c: DistanceX(g0,g4) = 4
    c: Coincident(g7,g-1)
    c: Radius(g7) = 1
FEATURE [Sketcher::SketchObject] Sketch2110
  MapMode = 5
  Support = -> [XY_Plane826]
FEATURE [Sketcher::SketchObject] Sketch2112
  MapMode = 5
  Support = -> [XY_Plane837]
  sketch-geometry (1):
    g0: Circle CenterX=0 CenterY=0 CenterZ=0 NormalX=0 NormalY=0 NormalZ=1 AngleXU=0 Radius=1.9
  constraints (2):
    c: Coincident(g0,g-1)
    c: Radius(g0) = 1.9
FEATURE [Sketcher::SketchObject] Sketch2114
  MapMode = 5
  Support = -> [XY_Plane826]
FEATURE [Sketcher::SketchObject] Sketch2115
  MapMode = 5
  Support = -> [XY_Plane836]
  sketch-geometry (8):
    g0: LineSegment StartX=0 StartY=2.3094 StartZ=0 EndX=-2 EndY=1.1547 EndZ=0
    g1: LineSegment StartX=-2 StartY=1.1547 StartZ=0 EndX=-2 EndY=-1.1547 EndZ=0
    g2: LineSegment StartX=-2 StartY=-1.1547 StartZ=0 EndX=-2e-16 EndY=-2.3094 EndZ=0
    g3: LineSegment StartX=-2e-16 StartY=-2.3094 StartZ=0 EndX=2 EndY=-1.1547 EndZ=0
    g4: LineSegment StartX=2 StartY=-1.1547 StartZ=0 EndX=2 EndY=1.1547 EndZ=0
    g5: LineSegment StartX=2 StartY=1.1547 StartZ=0 EndX=0 EndY=2.3094 EndZ=0
    g6: Circle [constr] CenterX=0 CenterY=0 CenterZ=0 NormalX=0 NormalY=0 NormalZ=1 AngleXU=0 Radius=2.3094
    g7: Circle CenterX=0 CenterY=0 CenterZ=0 NormalX=0 NormalY=0 NormalZ=1 AngleXU=0 Radius=1
  constraints (18):
    c: Coincident(g0,g1)
    c: Coincident(g1,g2)
    c: Coincident(g2,g3)
    c: Coincident(g3,g4)
    c: Coincident(g4,g5)
    c: Coincident(g5,g0)
    c: Equal(g0, g1-g5) x5
    c: PointOnObject(g0,g6)
    c: PointOnObject(g1,g6)
    c: PointOnObject(g2,g6)
    c: PointOnObject(g3,g6)
    c: PointOnObject(g4,g6)
    c: PointOnObject(g5,g6)
    c: Coincident(g6,g-1)
    c: PointOnObject(g5,g-2)
    c: DistanceX(g0,g4) = 4
    c: Coincident(g7,g-1)
    c: Radius(g7) = 1
FEATURE [Sketcher::SketchObject] Sketch2116
  MapMode = 5
  Support = -> [XY_Plane827]
FEATURE [Sketcher::SketchObject] Sketch2121
  MapMode = 5
  Support = -> [XY_Plane834]
  sketch-geometry (1):
    g0: Circle CenterX=0 CenterY=0 CenterZ=0 NormalX=0 NormalY=0 NormalZ=1 AngleXU=0 Radius=1.9
  constraints (2):
    c: Coincident(g0,g-1)
    c: Radius(g0) = 1.9
FEATURE [Sketcher::SketchObject] Sketch2125
  MapMode = 5
  Support = -> [XY_Plane826]
  sketch-geometry (8):
    g0: LineSegment StartX=0 StartY=2.3094 StartZ=0 EndX=-2 EndY=1.1547 EndZ=0
    g1: LineSegment StartX=-2 StartY=1.1547 StartZ=0 EndX=-2 EndY=-1.1547 EndZ=0
    g2: LineSegment StartX=-2 StartY=-1.1547 StartZ=0 EndX=-2e-16 EndY=-2.3094 EndZ=0
    g3: LineSegment StartX=-2e-16 StartY=-2.3094 StartZ=0 EndX=2 EndY=-1.1547 EndZ=0
    g4: LineSegment StartX=2 StartY=-1.1547 StartZ=0 EndX=2 EndY=1.1547 EndZ=0
    g5: LineSegment StartX=2 StartY=1.1547 StartZ=0 EndX=0 EndY=2.3094 EndZ=0
    g6: Circle [constr] CenterX=0 CenterY=0 CenterZ=0 NormalX=0 NormalY=0 NormalZ=1 AngleXU=0 Radius=2.3094
    g7: Circle CenterX=0 CenterY=0 CenterZ=0 NormalX=0 NormalY=0 NormalZ=1 AngleXU=0 Radius=1
  constraints (18):
    c: Coincident(g0,g1)
    c: Coincident(g1,g2)
    c: Coincident(g2,g3)
    c: Coincident(g3,g4)
    c: Coincident(g4,g5)
    c: Coincident(g5,g0)
    c: Equal(g0, g1-g5) x5
    c: PointOnObject(g0,g6)
    c: PointOnObject(g1,g6)
    c: PointOnObject(g2,g6)
    c: PointOnObject(g3,g6)
    c: PointOnObject(g4,g6)
    c: PointOnObject(g5,g6)
    c: Coincident(g6,g-1)
    c: PointOnObject(g5,g-2)
    c: DistanceX(g0,g4) = 4
    c: Coincident(g7,g-1)
    c: Radius(g7) = 1
FEATURE [Sketcher::SketchObject] Sketch2127
  MapMode = 5
  Support = -> [XY_Plane838]
FEATURE [Sketcher::SketchObject] Sketch2128
  MapMode = 5
  Support = -> [XY_Plane824]
  sketch-geometry (8):
    g0: LineSegment StartX=0 StartY=2.3094 StartZ=0 EndX=-2 EndY=1.1547 EndZ=0
    g1: LineSegment StartX=-2 StartY=1.1547 StartZ=0 EndX=-2 EndY=-1.1547 EndZ=0
    g2: LineSegment StartX=-2 StartY=-1.1547 StartZ=0 EndX=-2e-16 EndY=-2.3094 EndZ=0
    g3: LineSegment StartX=-2e-16 StartY=-2.3094 StartZ=0 EndX=2 EndY=-1.1547 EndZ=0
    g4: LineSegment StartX=2 StartY=-1.1547 StartZ=0 EndX=2 EndY=1.1547 EndZ=0
    g5: LineSegment StartX=2 StartY=1.1547 StartZ=0 EndX=0 EndY=2.3094 EndZ=0
    g6: Circle [constr] CenterX=0 CenterY=0 CenterZ=0 NormalX=0 NormalY=0 NormalZ=1 AngleXU=0 Radius=2.3094
    g7: Circle CenterX=0 CenterY=0 CenterZ=0 NormalX=0 NormalY=0 NormalZ=1 AngleXU=0 Radius=1
  constraints (18):
    c: Coincident(g0,g1)
    c: Coincident(g1,g2)
    c: Coincident(g2,g3)
    c: Coincident(g3,g4)
    c: Coincident(g4,g5)
    c: Coincident(g5,g0)
    c: Equal(g0, g1-g5) x5
    c: PointOnObject(g0,g6)
    c: PointOnObject(g1,g6)
    c: PointOnObject(g2,g6)
    c: PointOnObject(g3,g6)
    c: PointOnObject(g4,g6)
    c: PointOnObject(g5,g6)
    c: Coincident(g6,g-1)
    c: PointOnObject(g5,g-2)
    c: DistanceX(g0,g4) = 4
    c: Coincident(g7,g-1)
    c: Radius(g7) = 1
FEATURE [Sketcher::SketchObject] Sketch2130
  MapMode = 5
  Support = -> [XY_Plane836]
FEATURE [Sketcher::SketchObject] Sketch2132
  MapMode = 5
  Support = -> [XY_Plane824]
FEATURE [Sketcher::SketchObject] Sketch2135
  MapMode = 5
  Support = -> [XY_Plane824]
FEATURE [Sketcher::SketchObject] Sketch2136
  MapMode = 5
  Support = -> [XY_Plane836]
FEATURE [Sketcher::SketchObject] Sketch2138
  MapMode = 5
  Support = -> [XY_Plane840]
  sketch-geometry (1):
    g0: Circle CenterX=0 CenterY=0 CenterZ=0 NormalX=0 NormalY=0 NormalZ=1 AngleXU=0 Radius=1.9
  constraints (2):
    c: Coincident(g0,g-1)
    c: Radius(g0) = 1.9
FEATURE [Sketcher::SketchObject] Sketch2139
  MapMode = 5
  Support = -> [XY_Plane838]
FEATURE [PartDesign::Pad] Pad920  label="M3x8 Head119"
  Length = 2
  Length2 = 100
  Profile = -> Sketch2102
  Type = 0
FEATURE [Sketcher::SketchObject] Sketch2098
  MapMode = 5
  Placement = pos=(0,0,2) rot=(0,0,1;0rad)
  Support = -> [Pad920]
  sketch-geometry (1):
    g0: Circle CenterX=0 CenterY=0 CenterZ=0 NormalX=0 NormalY=0 NormalZ=1 AngleXU=0 Radius=1
  constraints (2):
    c: Coincident(g0,g-1)
    c: Radius(g0) = 1
FEATURE [PartDesign::Pad] Pad922  label="M3x8 Head120"
  Length = 2
  Length2 = 100
  Profile = -> Sketch2138
  Type = 0
FEATURE [Sketcher::SketchObject] Sketch2137
  MapMode = 5
  Placement = pos=(0,0,2) rot=(0,0,1;0rad)
  Support = -> [Pad922]
  sketch-geometry (1):
    g0: Circle CenterX=0 CenterY=0 CenterZ=0 NormalX=0 NormalY=0 NormalZ=1 AngleXU=0 Radius=1
  constraints (2):
    c: Coincident(g0,g-1)
    c: Radius(g0) = 1
FEATURE [PartDesign::Pad] Pad921  label="M3x8 Thread119"
  BaseFeature = -> Pad922
  Length = 8
  Length2 = 100
  Profile = -> Sketch2137
  Type = 0
FEATURE [Sketcher::SketchObject] Sketch2119
  MapMode = 5
  Placement = pos=(0,0,0) rot=(1,0,0;3.14159rad)
  Support = -> [Pad921]
  sketch-geometry (7):
    g0: LineSegment StartX=0.77 StartY=0.44456 StartZ=0 EndX=0 EndY=0.889119 EndZ=0
    g1: LineSegment StartX=0 StartY=0.889119 StartZ=0 EndX=-0.77 EndY=0.44456 EndZ=0
    g2: LineSegment StartX=-0.77 StartY=0.44456 StartZ=0 EndX=-0.77 EndY=-0.44456 EndZ=0
    g3: LineSegment StartX=-0.77 StartY=-0.44456 StartZ=0 EndX=3.85628e-11 EndY=-0.889119 EndZ=0
    g4: LineSegment StartX=3.85628e-11 StartY=-0.889119 StartZ=0 EndX=0.77 EndY=-0.44456 EndZ=0
    g5: LineSegment StartX=0.77 StartY=-0.44456 StartZ=0 EndX=0.77 EndY=0.44456 EndZ=0
    g6: Circle [constr] CenterX=0 CenterY=0 CenterZ=0 NormalX=0 NormalY=0 NormalZ=1 AngleXU=0 Radius=0.889119
  constraints (16):
    c: Coincident(g0,g1)
    c: Coincident(g1,g2)
    c: Coincident(g2,g3)
    c: Coincident(g3,g4)
    c: Coincident(g4,g5)
    c: Coincident(g5,g0)
    c: Equal(g0, g1-g5) x5
    c: PointOnObject(g0,g6)
    c: PointOnObject(g1,g6)
    c: PointOnObject(g2,g6)
    c: PointOnObject(g3,g6)
    c: PointOnObject(g4,g6)
    c: PointOnObject(g5,g6)
    c: Coincident(g6,g-1)
    c: PointOnObject(g0,g-2)
    c: DistanceX(g1,g0) = 1.54
FEATURE [PartDesign::Pad] Pad924  label="M3x8 Head121"
  Length = 2
  Length2 = 100
  Profile = -> Sketch2108
  Type = 0
FEATURE [Sketcher::SketchObject] Sketch2117
  MapMode = 5
  Placement = pos=(0,0,2) rot=(0,0,1;0rad)
  Support = -> [Pad924]
  sketch-geometry (1):
    g0: Circle CenterX=0 CenterY=0 CenterZ=0 NormalX=0 NormalY=0 NormalZ=1 AngleXU=0 Radius=1
  constraints (2):
    c: Coincident(g0,g-1)
    c: Radius(g0) = 1
FEATURE [PartDesign::Pad] Pad925  label="M3 Nut Primitive185"
  Length = 0.6
  Length2 = 0.6
  Profile = -> Sketch2125
  Type = 4
FEATURE [Sketcher::SketchObject] Sketch2111
  ExternalGeometry = -> [Pad925]
  MapMode = 5
  Placement = pos=(0,0,0) rot=(0.57735,0.57735,0.57735;2.0944rad)
  Support = -> [YZ_Plane823]
  sketch-geometry (6):
    g0: LineSegment StartX=-1.9594 StartY=0.6 StartZ=0 EndX=-2.8094 EndY=0.6 EndZ=0
    g1: LineSegment StartX=-2.8094 StartY=0.6 StartZ=0 EndX=-2.8094 EndY=-0.6 EndZ=0
    g2: LineSegment StartX=-2.8094 StartY=-0.6 StartZ=0 EndX=-1.9594 EndY=-0.6 EndZ=0
    g3: LineSegment StartX=-1.9594 StartY=-0.6 StartZ=0 EndX=-2.3094 EndY=-0.4 EndZ=0
    g4: LineSegment StartX=-2.3094 StartY=-0.4 StartZ=0 EndX=-2.3094 EndY=0.4 EndZ=0
    g5: LineSegment StartX=-2.3094 StartY=0.4 StartZ=0 EndX=-1.9594 EndY=0.6 EndZ=0
  constraints (15):
    c: Horizontal(g0)
    c: Coincident(g0,g1)
    c: Coincident(g1,g2)
    c: Coincident(g2,g3)
    c: Coincident(g3,g4)
    c: Coincident(g4,g5)
    c: Coincident(g5,g0)
    c: Symmetric(g4,g3,g-1)
    c: Symmetric(g0,g2,g-1)
    c: Symmetric(g1,g0,g-1)
    c: DistanceX(g0,g4) = 0.5
    c: DistanceY(g3,g4) = 0.8
    c: DistanceY(g1,g0) = 1.2
    c: PointOnObject(g3,g-3)
    c: DistanceX(g4,g0) = 0.35
FEATURE [PartDesign::Pad] Pad926  label="M3x8 Thread120"
  BaseFeature = -> Pad920
  Length = 8
  Length2 = 100
  Profile = -> Sketch2098
  Type = 0
FEATURE [Sketcher::SketchObject] Sketch2103
  MapMode = 5
  Placement = pos=(0,0,0) rot=(1,0,0;3.14159rad)
  Support = -> [Pad926]
  sketch-geometry (7):
    g0: LineSegment StartX=0.77 StartY=0.44456 StartZ=0 EndX=0 EndY=0.889119 EndZ=0
    g1: LineSegment StartX=0 StartY=0.889119 StartZ=0 EndX=-0.77 EndY=0.44456 EndZ=0
    g2: LineSegment StartX=-0.77 StartY=0.44456 StartZ=0 EndX=-0.77 EndY=-0.44456 EndZ=0
    g3: LineSegment StartX=-0.77 StartY=-0.44456 StartZ=0 EndX=3.85628e-11 EndY=-0.889119 EndZ=0
    g4: LineSegment StartX=3.85628e-11 StartY=-0.889119 StartZ=0 EndX=0.77 EndY=-0.44456 EndZ=0
    g5: LineSegment StartX=0.77 StartY=-0.44456 StartZ=0 EndX=0.77 EndY=0.44456 EndZ=0
    g6: Circle [constr] CenterX=0 CenterY=0 CenterZ=0 NormalX=0 NormalY=0 NormalZ=1 AngleXU=0 Radius=0.889119
  constraints (16):
    c: Coincident(g0,g1)
    c: Coincident(g1,g2)
    c: Coincident(g2,g3)
    c: Coincident(g3,g4)
    c: Coincident(g4,g5)
    c: Coincident(g5,g0)
    c: Equal(g0, g1-g5) x5
    c: PointOnObject(g0,g6)
    c: PointOnObject(g1,g6)
    c: PointOnObject(g2,g6)
    c: PointOnObject(g3,g6)
    c: PointOnObject(g4,g6)
    c: PointOnObject(g5,g6)
    c: Coincident(g6,g-1)
    c: PointOnObject(g0,g-2)
    c: DistanceX(g1,g0) = 1.54
FEATURE [PartDesign::Pocket] Pocket758  label="M3x8 Wrench120"
  BaseFeature = -> Pad921
  Length = 1
  Length2 = 100
  Profile = -> Sketch2119
  Type = 0
FEATURE [PartDesign::Chamfer] Chamfer442  label="M3x8 Smooth120"
  Base = -> Pocket758 [Face11,Edge2,Edge24,Edge3]
  BaseFeature = -> Pocket758
  Size = 0.2
FEATURE [PartDesign::Pad] Pad927  label="M3x8 Thread121"
  BaseFeature = -> Pad924
  Length = 8
  Length2 = 100
  Profile = -> Sketch2117
  Type = 0
FEATURE [Sketcher::SketchObject] Sketch2124
  MapMode = 5
  Placement = pos=(0,0,0) rot=(1,0,0;3.14159rad)
  Support = -> [Pad927]
  sketch-geometry (7):
    g0: LineSegment StartX=0.77 StartY=0.44456 StartZ=0 EndX=0 EndY=0.889119 EndZ=0
    g1: LineSegment StartX=0 StartY=0.889119 StartZ=0 EndX=-0.77 EndY=0.44456 EndZ=0
    g2: LineSegment StartX=-0.77 StartY=0.44456 StartZ=0 EndX=-0.77 EndY=-0.44456 EndZ=0
    g3: LineSegment StartX=-0.77 StartY=-0.44456 StartZ=0 EndX=3.85628e-11 EndY=-0.889119 EndZ=0
    g4: LineSegment StartX=3.85628e-11 StartY=-0.889119 StartZ=0 EndX=0.77 EndY=-0.44456 EndZ=0
    g5: LineSegment StartX=0.77 StartY=-0.44456 StartZ=0 EndX=0.77 EndY=0.44456 EndZ=0
    g6: Circle [constr] CenterX=0 CenterY=0 CenterZ=0 NormalX=0 NormalY=0 NormalZ=1 AngleXU=0 Radius=0.889119
  constraints (16):
    c: Coincident(g0,g1)
    c: Coincident(g1,g2)
    c: Coincident(g2,g3)
    c: Coincident(g3,g4)
    c: Coincident(g4,g5)
    c: Coincident(g5,g0)
    c: Equal(g0, g1-g5) x5
    c: PointOnObject(g0,g6)
    c: PointOnObject(g1,g6)
    c: PointOnObject(g2,g6)
    c: PointOnObject(g3,g6)
    c: PointOnObject(g4,g6)
    c: PointOnObject(g5,g6)
    c: Coincident(g6,g-1)
    c: PointOnObject(g0,g-2)
    c: DistanceX(g1,g0) = 1.54
FEATURE [PartDesign::Groove] Groove197  label="M3 Nut Smooth189"
  Angle = 360
  Axis = (-2e-16,3e-16,1)
  Base = (0,0,0)
  BaseFeature = -> Pad925
  Profile = -> Sketch2111
  ReferenceAxis = -> Sketch2111 [V_Axis]
  Reversed = true
FEATURE [PartDesign::Chamfer] Chamfer438  label="M3 Nut Smooth Hole187"
  Base = -> Groove197 [Edge24,Edge23]
  BaseFeature = -> Groove197
  Size = 0.2
FEATURE [PartDesign::Pad] Pad928  label="M3x8 Head122"
  Length = 2
  Length2 = 100
  Profile = -> Sketch2121
  Type = 0
FEATURE [Sketcher::SketchObject] Sketch2131
  MapMode = 5
  Placement = pos=(0,0,2) rot=(0,0,1;0rad)
  Support = -> [Pad928]
  sketch-geometry (1):
    g0: Circle CenterX=0 CenterY=0 CenterZ=0 NormalX=0 NormalY=0 NormalZ=1 AngleXU=0 Radius=1
  constraints (2):
    c: Coincident(g0,g-1)
    c: Radius(g0) = 1
FEATURE [PartDesign::Pad] Pad929  label="M3x8 Head123"
  Length = 2
  Length2 = 100
  Profile = -> Sketch2112
  Type = 0
FEATURE [Sketcher::SketchObject] Sketch2120
  MapMode = 5
  Placement = pos=(0,0,2) rot=(0,0,1;0rad)
  Support = -> [Pad929]
  sketch-geometry (1):
    g0: Circle CenterX=0 CenterY=0 CenterZ=0 NormalX=0 NormalY=0 NormalZ=1 AngleXU=0 Radius=1
  constraints (2):
    c: Coincident(g0,g-1)
    c: Radius(g0) = 1
FEATURE [PartDesign::Pad] Pad930  label="M3 Nut Primitive186"
  Length = 0.6
  Length2 = 0.6
  Profile = -> Sketch2104
  Type = 4
FEATURE [Sketcher::SketchObject] Sketch2118
  ExternalGeometry = -> [Pad930]
  MapMode = 5
  Placement = pos=(0,0,0) rot=(0.57735,0.57735,0.57735;2.0944rad)
  Support = -> [YZ_Plane821]
  sketch-geometry (6):
    g0: LineSegment StartX=-1.9594 StartY=0.6 StartZ=0 EndX=-2.8094 EndY=0.6 EndZ=0
    g1: LineSegment StartX=-2.8094 StartY=0.6 StartZ=0 EndX=-2.8094 EndY=-0.6 EndZ=0
    g2: LineSegment StartX=-2.8094 StartY=-0.6 StartZ=0 EndX=-1.9594 EndY=-0.6 EndZ=0
    g3: LineSegment StartX=-1.9594 StartY=-0.6 StartZ=0 EndX=-2.3094 EndY=-0.4 EndZ=0
    g4: LineSegment StartX=-2.3094 StartY=-0.4 StartZ=0 EndX=-2.3094 EndY=0.4 EndZ=0
    g5: LineSegment StartX=-2.3094 StartY=0.4 StartZ=0 EndX=-1.9594 EndY=0.6 EndZ=0
  constraints (15):
    c: Horizontal(g0)
    c: Coincident(g0,g1)
    c: Coincident(g1,g2)
    c: Coincident(g2,g3)
    c: Coincident(g3,g4)
    c: Coincident(g4,g5)
    c: Coincident(g5,g0)
    c: Symmetric(g4,g3,g-1)
    c: Symmetric(g0,g2,g-1)
    c: Symmetric(g1,g0,g-1)
    c: DistanceX(g0,g4) = 0.5
    c: DistanceY(g3,g4) = 0.8
    c: DistanceY(g1,g0) = 1.2
    c: PointOnObject(g3,g-3)
    c: DistanceX(g4,g0) = 0.35
FEATURE [PartDesign::Groove] Groove194  label="M3 Nut Smooth186"
  Angle = 360
  Axis = (-2e-16,3e-16,1)
  Base = (0,0,0)
  BaseFeature = -> Pad930
  Profile = -> Sketch2118
  ReferenceAxis = -> Sketch2118 [V_Axis]
  Reversed = true
FEATURE [PartDesign::Chamfer] Chamfer437  label="M3 Nut Smooth Hole186"
  Base = -> Groove194 [Edge24,Edge23]
  BaseFeature = -> Groove194
  Size = 0.2
FEATURE [PartDesign::Pad] Pad931  label="M3x8 Head124"
  Length = 2
  Length2 = 100
  Profile = -> Sketch2107
  Type = 0
FEATURE [Sketcher::SketchObject] Sketch2122
  MapMode = 5
  Placement = pos=(0,0,2) rot=(0,0,1;0rad)
  Support = -> [Pad931]
  sketch-geometry (1):
    g0: Circle CenterX=0 CenterY=0 CenterZ=0 NormalX=0 NormalY=0 NormalZ=1 AngleXU=0 Radius=1
  constraints (2):
    c: Coincident(g0,g-1)
    c: Radius(g0) = 1
FEATURE [PartDesign::Pad] Pad932  label="M3 Nut Primitive187"
  Length = 0.6
  Length2 = 0.6
  Profile = -> Sketch2105
  Type = 4
FEATURE [Sketcher::SketchObject] Sketch2101
  ExternalGeometry = -> [Pad932]
  MapMode = 5
  Placement = pos=(0,0,0) rot=(0.57735,0.57735,0.57735;2.0944rad)
  Support = -> [YZ_Plane833]
  sketch-geometry (6):
    g0: LineSegment StartX=-1.9594 StartY=0.6 StartZ=0 EndX=-2.8094 EndY=0.6 EndZ=0
    g1: LineSegment StartX=-2.8094 StartY=0.6 StartZ=0 EndX=-2.8094 EndY=-0.6 EndZ=0
    g2: LineSegment StartX=-2.8094 StartY=-0.6 StartZ=0 EndX=-1.9594 EndY=-0.6 EndZ=0
    g3: LineSegment StartX=-1.9594 StartY=-0.6 StartZ=0 EndX=-2.3094 EndY=-0.4 EndZ=0
    g4: LineSegment StartX=-2.3094 StartY=-0.4 StartZ=0 EndX=-2.3094 EndY=0.4 EndZ=0
    g5: LineSegment StartX=-2.3094 StartY=0.4 StartZ=0 EndX=-1.9594 EndY=0.6 EndZ=0
  constraints (15):
    c: Horizontal(g0)
    c: Coincident(g0,g1)
    c: Coincident(g1,g2)
    c: Coincident(g2,g3)
    c: Coincident(g3,g4)
    c: Coincident(g4,g5)
    c: Coincident(g5,g0)
    c: Symmetric(g4,g3,g-1)
    c: Symmetric(g0,g2,g-1)
    c: Symmetric(g1,g0,g-1)
    c: DistanceX(g0,g4) = 0.5
    c: DistanceY(g3,g4) = 0.8
    c: DistanceY(g1,g0) = 1.2
    c: PointOnObject(g3,g-3)
    c: DistanceX(g4,g0) = 0.35
FEATURE [PartDesign::Groove] Groove196  label="M3 Nut Smooth188"
  Angle = 360
  Axis = (-2e-16,3e-16,1)
  Base = (0,0,0)
  BaseFeature = -> Pad932
  Profile = -> Sketch2101
  ReferenceAxis = -> Sketch2101 [V_Axis]
  Reversed = true
FEATURE [PartDesign::Chamfer] Chamfer444  label="M3 Nut Smooth Hole189"
  Base = -> Groove196 [Edge24,Edge23]
  BaseFeature = -> Groove196
  Size = 0.2
FEATURE [PartDesign::Pocket] Pocket761  label="M3x8 Wrench122"
  BaseFeature = -> Pad926
  Length = 1
  Length2 = 100
  Profile = -> Sketch2103
  Type = 0
FEATURE [PartDesign::Chamfer] Chamfer445  label="M3x8 Smooth122"
  Base = -> Pocket761 [Face11,Edge2,Edge24,Edge3]
  BaseFeature = -> Pocket761
  Size = 0.2
FEATURE [PartDesign::Pocket] Pocket762  label="M3x8 Wrench123"
  BaseFeature = -> Pad927
  Length = 1
  Length2 = 100
  Profile = -> Sketch2124
  Type = 0
FEATURE [PartDesign::Chamfer] Chamfer443  label="M3x8 Smooth121"
  Base = -> Pocket762 [Face11,Edge2,Edge24,Edge3]
  BaseFeature = -> Pocket762
  Size = 0.2
FEATURE [PartDesign::Pad] Pad933  label="M3x8 Thread122"
  BaseFeature = -> Pad931
  Length = 8
  Length2 = 100
  Profile = -> Sketch2122
  Type = 0
FEATURE [Sketcher::SketchObject] Sketch2123
  MapMode = 5
  Placement = pos=(0,0,0) rot=(1,0,0;3.14159rad)
  Support = -> [Pad933]
  sketch-geometry (7):
    g0: LineSegment StartX=0.77 StartY=0.44456 StartZ=0 EndX=0 EndY=0.889119 EndZ=0
    g1: LineSegment StartX=0 StartY=0.889119 StartZ=0 EndX=-0.77 EndY=0.44456 EndZ=0
    g2: LineSegment StartX=-0.77 StartY=0.44456 StartZ=0 EndX=-0.77 EndY=-0.44456 EndZ=0
    g3: LineSegment StartX=-0.77 StartY=-0.44456 StartZ=0 EndX=3.85628e-11 EndY=-0.889119 EndZ=0
    g4: LineSegment StartX=3.85628e-11 StartY=-0.889119 StartZ=0 EndX=0.77 EndY=-0.44456 EndZ=0
    g5: LineSegment StartX=0.77 StartY=-0.44456 StartZ=0 EndX=0.77 EndY=0.44456 EndZ=0
    g6: Circle [constr] CenterX=0 CenterY=0 CenterZ=0 NormalX=0 NormalY=0 NormalZ=1 AngleXU=0 Radius=0.889119
  constraints (16):
    c: Coincident(g0,g1)
    c: Coincident(g1,g2)
    c: Coincident(g2,g3)
    c: Coincident(g3,g4)
    c: Coincident(g4,g5)
    c: Coincident(g5,g0)
    c: Equal(g0, g1-g5) x5
    c: PointOnObject(g0,g6)
    c: PointOnObject(g1,g6)
    c: PointOnObject(g2,g6)
    c: PointOnObject(g3,g6)
    c: PointOnObject(g4,g6)
    c: PointOnObject(g5,g6)
    c: Coincident(g6,g-1)
    c: PointOnObject(g0,g-2)
    c: DistanceX(g1,g0) = 1.54
FEATURE [PartDesign::Pocket] Pocket757  label="M3x8 Wrench119"
  BaseFeature = -> Pad933
  Length = 1
  Length2 = 100
  Profile = -> Sketch2123
  Type = 0
FEATURE [PartDesign::Chamfer] Chamfer447  label="M3x8 Smooth123"
  Base = -> Pocket757 [Face11,Edge2,Edge24,Edge3]
  BaseFeature = -> Pocket757
  Size = 0.2
FEATURE [PartDesign::Pad] Pad934  label="M3x8 Thread123"
  BaseFeature = -> Pad929
  Length = 8
  Length2 = 100
  Profile = -> Sketch2120
  Type = 0
FEATURE [Sketcher::SketchObject] Sketch2113
  MapMode = 5
  Placement = pos=(0,0,0) rot=(1,0,0;3.14159rad)
  Support = -> [Pad934]
  sketch-geometry (7):
    g0: LineSegment StartX=0.77 StartY=0.44456 StartZ=0 EndX=0 EndY=0.889119 EndZ=0
    g1: LineSegment StartX=0 StartY=0.889119 StartZ=0 EndX=-0.77 EndY=0.44456 EndZ=0
    g2: LineSegment StartX=-0.77 StartY=0.44456 StartZ=0 EndX=-0.77 EndY=-0.44456 EndZ=0
    g3: LineSegment StartX=-0.77 StartY=-0.44456 StartZ=0 EndX=3.85628e-11 EndY=-0.889119 EndZ=0
    g4: LineSegment StartX=3.85628e-11 StartY=-0.889119 StartZ=0 EndX=0.77 EndY=-0.44456 EndZ=0
    g5: LineSegment StartX=0.77 StartY=-0.44456 StartZ=0 EndX=0.77 EndY=0.44456 EndZ=0
    g6: Circle [constr] CenterX=0 CenterY=0 CenterZ=0 NormalX=0 NormalY=0 NormalZ=1 AngleXU=0 Radius=0.889119
  constraints (16):
    c: Coincident(g0,g1)
    c: Coincident(g1,g2)
    c: Coincident(g2,g3)
    c: Coincident(g3,g4)
    c: Coincident(g4,g5)
    c: Coincident(g5,g0)
    c: Equal(g0, g1-g5) x5
    c: PointOnObject(g0,g6)
    c: PointOnObject(g1,g6)
    c: PointOnObject(g2,g6)
    c: PointOnObject(g3,g6)
    c: PointOnObject(g4,g6)
    c: PointOnObject(g5,g6)
    c: Coincident(g6,g-1)
    c: PointOnObject(g0,g-2)
    c: DistanceX(g1,g0) = 1.54
FEATURE [PartDesign::Pocket] Pocket760  label="M3x8 Wrench121"
  BaseFeature = -> Pad934
  Length = 1
  Length2 = 100
  Profile = -> Sketch2113
  Type = 0
FEATURE [PartDesign::Chamfer] Chamfer439  label="M3x8 Smooth118"
  Base = -> Pocket760 [Face11,Edge2,Edge24,Edge3]
  BaseFeature = -> Pocket760
  Size = 0.2
FEATURE [PartDesign::Pad] Pad935  label="M3 Nut Primitive188"
  Length = 0.6
  Length2 = 0.6
  Profile = -> Sketch2109
  Type = 4
FEATURE [Sketcher::SketchObject] Sketch2129
  ExternalGeometry = -> [Pad935]
  MapMode = 5
  Placement = pos=(0,0,0) rot=(0.57735,0.57735,0.57735;2.0944rad)
  Support = -> [YZ_Plane831]
  sketch-geometry (6):
    g0: LineSegment StartX=-1.9594 StartY=0.6 StartZ=0 EndX=-2.8094 EndY=0.6 EndZ=0
    g1: LineSegment StartX=-2.8094 StartY=0.6 StartZ=0 EndX=-2.8094 EndY=-0.6 EndZ=0
    g2: LineSegment StartX=-2.8094 StartY=-0.6 StartZ=0 EndX=-1.9594 EndY=-0.6 EndZ=0
    g3: LineSegment StartX=-1.9594 StartY=-0.6 StartZ=0 EndX=-2.3094 EndY=-0.4 EndZ=0
    g4: LineSegment StartX=-2.3094 StartY=-0.4 StartZ=0 EndX=-2.3094 EndY=0.4 EndZ=0
    g5: LineSegment StartX=-2.3094 StartY=0.4 StartZ=0 EndX=-1.9594 EndY=0.6 EndZ=0
  constraints (15):
    c: Horizontal(g0)
    c: Coincident(g0,g1)
    c: Coincident(g1,g2)
    c: Coincident(g2,g3)
    c: Coincident(g3,g4)
    c: Coincident(g4,g5)
    c: Coincident(g5,g0)
    c: Symmetric(g4,g3,g-1)
    c: Symmetric(g0,g2,g-1)
    c: Symmetric(g1,g0,g-1)
    c: DistanceX(g0,g4) = 0.5
    c: DistanceY(g3,g4) = 0.8
    c: DistanceY(g1,g0) = 1.2
    c: PointOnObject(g3,g-3)
    c: DistanceX(g4,g0) = 0.35
FEATURE [PartDesign::Groove] Groove193  label="M3 Nut Smooth185"
  Angle = 360
  Axis = (-2e-16,3e-16,1)
  Base = (0,0,0)
  BaseFeature = -> Pad935
  Profile = -> Sketch2129
  ReferenceAxis = -> Sketch2129 [V_Axis]
  Reversed = true
FEATURE [PartDesign::Chamfer] Chamfer446  label="M3 Nut Smooth Hole190"
  Base = -> Groove193 [Edge24,Edge23]
  BaseFeature = -> Groove193
  Size = 0.2
FEATURE [PartDesign::Pad] Pad936  label="M3 Nut Primitive189"
  Length = 0.6
  Length2 = 0.6
  Profile = -> Sketch2115
  Type = 4
FEATURE [Sketcher::SketchObject] Sketch2126
  ExternalGeometry = -> [Pad936]
  MapMode = 5
  Placement = pos=(0,0,0) rot=(0.57735,0.57735,0.57735;2.0944rad)
  Support = -> [YZ_Plane834]
  sketch-geometry (6):
    g0: LineSegment StartX=-1.9594 StartY=0.6 StartZ=0 EndX=-2.8094 EndY=0.6 EndZ=0
    g1: LineSegment StartX=-2.8094 StartY=0.6 StartZ=0 EndX=-2.8094 EndY=-0.6 EndZ=0
    g2: LineSegment StartX=-2.8094 StartY=-0.6 StartZ=0 EndX=-1.9594 EndY=-0.6 EndZ=0
    g3: LineSegment StartX=-1.9594 StartY=-0.6 StartZ=0 EndX=-2.3094 EndY=-0.4 EndZ=0
    g4: LineSegment StartX=-2.3094 StartY=-0.4 StartZ=0 EndX=-2.3094 EndY=0.4 EndZ=0
    g5: LineSegment StartX=-2.3094 StartY=0.4 StartZ=0 EndX=-1.9594 EndY=0.6 EndZ=0
  constraints (15):
    c: Horizontal(g0)
    c: Coincident(g0,g1)
    c: Coincident(g1,g2)
    c: Coincident(g2,g3)
    c: Coincident(g3,g4)
    c: Coincident(g4,g5)
    c: Coincident(g5,g0)
    c: Symmetric(g4,g3,g-1)
    c: Symmetric(g0,g2,g-1)
    c: Symmetric(g1,g0,g-1)
    c: DistanceX(g0,g4) = 0.5
    c: DistanceY(g3,g4) = 0.8
    c: DistanceY(g1,g0) = 1.2
    c: PointOnObject(g3,g-3)
    c: DistanceX(g4,g0) = 0.35
FEATURE [PartDesign::Groove] Groove195  label="M3 Nut Smooth187"
  Angle = 360
  Axis = (-2e-16,3e-16,1)
  Base = (0,0,0)
  BaseFeature = -> Pad936
  Profile = -> Sketch2126
  ReferenceAxis = -> Sketch2126 [V_Axis]
  Reversed = true
FEATURE [PartDesign::Chamfer] Chamfer436  label="M3 Nut Smooth Hole185"
  Base = -> Groove195 [Edge24,Edge23]
  BaseFeature = -> Groove195
  Size = 0.2
FEATURE [PartDesign::Pad] Pad937  label="M3x8 Thread124"
  BaseFeature = -> Pad928
  Length = 8
  Length2 = 100
  Profile = -> Sketch2131
  Type = 0
FEATURE [Sketcher::SketchObject] Sketch2133
  MapMode = 5
  Placement = pos=(0,0,0) rot=(1,0,0;3.14159rad)
  Support = -> [Pad937]
  sketch-geometry (7):
    g0: LineSegment StartX=0.77 StartY=0.44456 StartZ=0 EndX=0 EndY=0.889119 EndZ=0
    g1: LineSegment StartX=0 StartY=0.889119 StartZ=0 EndX=-0.77 EndY=0.44456 EndZ=0
    g2: LineSegment StartX=-0.77 StartY=0.44456 StartZ=0 EndX=-0.77 EndY=-0.44456 EndZ=0
    g3: LineSegment StartX=-0.77 StartY=-0.44456 StartZ=0 EndX=3.85628e-11 EndY=-0.889119 EndZ=0
    g4: LineSegment StartX=3.85628e-11 StartY=-0.889119 StartZ=0 EndX=0.77 EndY=-0.44456 EndZ=0
    g5: LineSegment StartX=0.77 StartY=-0.44456 StartZ=0 EndX=0.77 EndY=0.44456 EndZ=0
    g6: Circle [constr] CenterX=0 CenterY=0 CenterZ=0 NormalX=0 NormalY=0 NormalZ=1 AngleXU=0 Radius=0.889119
  constraints (16):
    c: Coincident(g0,g1)
    c: Coincident(g1,g2)
    c: Coincident(g2,g3)
    c: Coincident(g3,g4)
    c: Coincident(g4,g5)
    c: Coincident(g5,g0)
    c: Equal(g0, g1-g5) x5
    c: PointOnObject(g0,g6)
    c: PointOnObject(g1,g6)
    c: PointOnObject(g2,g6)
    c: PointOnObject(g3,g6)
    c: PointOnObject(g4,g6)
    c: PointOnObject(g5,g6)
    c: Coincident(g6,g-1)
    c: PointOnObject(g0,g-2)
    c: DistanceX(g1,g0) = 1.54
FEATURE [PartDesign::Pocket] Pocket763  label="M3x8 Wrench124"
  BaseFeature = -> Pad937
  Length = 1
  Length2 = 100
  Profile = -> Sketch2133
  Type = 0
FEATURE [PartDesign::Chamfer] Chamfer441  label="M3x8 Smooth119"
  Base = -> Pocket763 [Face11,Edge2,Edge24,Edge3]
  BaseFeature = -> Pocket763
  Size = 0.2
FEATURE [PartDesign::Pad] Pad938  label="M3 Nut Primitive190"
  Length = 0.6
  Length2 = 0.6
  Profile = -> Sketch2128
  Type = 4
FEATURE [Sketcher::SketchObject] Sketch2134
  ExternalGeometry = -> [Pad938]
  MapMode = 5
  Placement = pos=(0,0,0) rot=(0.57735,0.57735,0.57735;2.0944rad)
  Support = -> [YZ_Plane825]
  sketch-geometry (6):
    g0: LineSegment StartX=-1.9594 StartY=0.6 StartZ=0 EndX=-2.8094 EndY=0.6 EndZ=0
    g1: LineSegment StartX=-2.8094 StartY=0.6 StartZ=0 EndX=-2.8094 EndY=-0.6 EndZ=0
    g2: LineSegment StartX=-2.8094 StartY=-0.6 StartZ=0 EndX=-1.9594 EndY=-0.6 EndZ=0
    g3: LineSegment StartX=-1.9594 StartY=-0.6 StartZ=0 EndX=-2.3094 EndY=-0.4 EndZ=0
    g4: LineSegment StartX=-2.3094 StartY=-0.4 StartZ=0 EndX=-2.3094 EndY=0.4 EndZ=0
    g5: LineSegment StartX=-2.3094 StartY=0.4 StartZ=0 EndX=-1.9594 EndY=0.6 EndZ=0
  constraints (15):
    c: Horizontal(g0)
    c: Coincident(g0,g1)
    c: Coincident(g1,g2)
    c: Coincident(g2,g3)
    c: Coincident(g3,g4)
    c: Coincident(g4,g5)
    c: Coincident(g5,g0)
    c: Symmetric(g4,g3,g-1)
    c: Symmetric(g0,g2,g-1)
    c: Symmetric(g1,g0,g-1)
    c: DistanceX(g0,g4) = 0.5
    c: DistanceY(g3,g4) = 0.8
    c: DistanceY(g1,g0) = 1.2
    c: PointOnObject(g3,g-3)
    c: DistanceX(g4,g0) = 0.35
FEATURE [PartDesign::Groove] Groove198  label="M3 Nut Smooth190"
  Angle = 360
  Axis = (-2e-16,3e-16,1)
  Base = (0,0,0)
  BaseFeature = -> Pad938
  Profile = -> Sketch2134
  ReferenceAxis = -> Sketch2134 [V_Axis]
  Reversed = true
FEATURE [PartDesign::Chamfer] Chamfer440  label="M3 Nut Smooth Hole188"
  Base = -> Groove198 [Edge24,Edge23]
  BaseFeature = -> Groove198
  Size = 0.2
FEATURE [Sketcher::SketchObject] Sketch2143
  MapMode = 5
  Support = -> [XY_Plane831]
  sketch-geometry (64):
    g0: LineSegment [constr] StartX=-3.75 StartY=6.49519 StartZ=0 EndX=-7.5 EndY=0 EndZ=0
    g1: LineSegment [constr] StartX=-7.5 StartY=0 StartZ=0 EndX=-3.75 EndY=-6.49519 EndZ=0
    g2: LineSegment [constr] StartX=-3.75 StartY=-6.49519 StartZ=0 EndX=3.75 EndY=-6.49519 EndZ=0
    g3: LineSegment [constr] StartX=3.75 StartY=-6.49519 StartZ=0 EndX=7.5 EndY=0 EndZ=0
    g4: LineSegment [constr] StartX=7.5 StartY=0 StartZ=0 EndX=3.75 EndY=6.49519 EndZ=0
    g5: LineSegment [constr] StartX=3.75 StartY=6.49519 StartZ=0 EndX=-3.75 EndY=6.49519 EndZ=0
    g6: Circle [constr] CenterX=0 CenterY=0 CenterZ=0 NormalX=0 NormalY=0 NormalZ=1 AngleXU=0 Radius=7.5
    g7: LineSegment [constr] StartX=0 StartY=7.5 StartZ=0 EndX=-6.49519 EndY=3.75 EndZ=0
    g8: LineSegment [constr] StartX=-6.49519 StartY=3.75 StartZ=0 EndX=-6.49519 EndY=-3.75 EndZ=0
    g9: LineSegment [constr] StartX=-6.49519 StartY=-3.75 StartZ=0 EndX=9.8e-15 EndY=-7.5 EndZ=0
    g10: LineSegment [constr] StartX=9.8e-15 StartY=-7.5 StartZ=0 EndX=6.49519 EndY=-3.75 EndZ=0
    g11: LineSegment [constr] StartX=6.49519 StartY=-3.75 StartZ=0 EndX=6.49519 EndY=3.75 EndZ=0
    g12: LineSegment [constr] StartX=6.49519 StartY=3.75 StartZ=0 EndX=0 EndY=7.5 EndZ=0
    g13: Circle [constr] CenterX=0 CenterY=0 CenterZ=0 NormalX=0 NormalY=0 NormalZ=1 AngleXU=0 Radius=7.5
    g14: LineSegment [constr] StartX=0 StartY=10.5 StartZ=0 EndX=-9.09327 EndY=5.25 EndZ=0
    g15: LineSegment [constr] StartX=-9.09327 StartY=5.25 StartZ=0 EndX=-9.09327 EndY=-5.25 EndZ=0
    g16: LineSegment [constr] StartX=-9.09327 StartY=-5.25 StartZ=0 EndX=-1.42e-14 EndY=-10.5 EndZ=0
    g17: LineSegment [constr] StartX=-1.42e-14 StartY=-10.5 StartZ=0 EndX=9.09327 EndY=-5.25 EndZ=0
    g18: LineSegment [constr] StartX=9.09327 StartY=-5.25 StartZ=0 EndX=9.09327 EndY=5.25 EndZ=0
    g19: LineSegment [constr] StartX=9.09327 StartY=5.25 StartZ=0 EndX=0 EndY=10.5 EndZ=0
    g20: Circle [constr] CenterX=0 CenterY=0 CenterZ=0 NormalX=0 NormalY=0 NormalZ=1 AngleXU=0 Radius=10.5
    g21: LineSegment [constr] StartX=0 StartY=13.5 StartZ=0 EndX=-11.6913 EndY=6.75 EndZ=0
    g22: LineSegment [constr] StartX=-11.6913 StartY=6.75 StartZ=0 EndX=-11.6913 EndY=-6.75 EndZ=0
    g23: LineSegment [constr] StartX=-11.6913 StartY=-6.75 StartZ=0 EndX=0 EndY=-13.5 EndZ=0
    g24: LineSegment [constr] StartX=0 StartY=-13.5 StartZ=0 EndX=11.6913 EndY=-6.75 EndZ=0
    g25: LineSegment [constr] StartX=11.6913 StartY=-6.75 StartZ=0 EndX=11.6913 EndY=6.75 EndZ=0
    g26: LineSegment [constr] StartX=11.6913 StartY=6.75 StartZ=0 EndX=0 EndY=13.5 EndZ=0
    g27: Circle [constr] CenterX=0 CenterY=0 CenterZ=0 NormalX=0 NormalY=0 NormalZ=1 AngleXU=0 Radius=13.5
    g28: ArcOfCircle CenterX=0 CenterY=13.5 CenterZ=0 NormalX=0 NormalY=0 NormalZ=1 AngleXU=0 Radius=2.5 StartAngle=0.171439 EndAngle=2.97015
    g29: ArcOfCircle CenterX=11.6913 CenterY=6.75 CenterZ=0 NormalX=0 NormalY=0 NormalZ=1 AngleXU=0 Radius=2.5 StartAngle=5.40743 EndAngle=8.20614
    g30: ArcOfCircle CenterX=11.6913 CenterY=-6.75 CenterZ=0 NormalX=0 NormalY=0 NormalZ=1 AngleXU=0 Radius=2.5 StartAngle=4.36023 EndAngle=7.15894
    g31: ArcOfCircle CenterX=0 CenterY=-13.5 CenterZ=0 NormalX=0 NormalY=0 NormalZ=1 AngleXU=0 Radius=2.5 StartAngle=3.31303 EndAngle=6.11175
    g32: ArcOfCircle CenterX=-11.6913 CenterY=-6.75 CenterZ=0 NormalX=0 NormalY=0 NormalZ=1 AngleXU=0 Radius=2.5 StartAngle=2.26583 EndAngle=5.06455
    g33: ArcOfCircle CenterX=-11.6913 CenterY=6.75 CenterZ=0 NormalX=0 NormalY=0 NormalZ=1 AngleXU=0 Radius=2.5 StartAngle=1.21864 EndAngle=4.01735
    g34: LineSegment StartX=-10.829 StartY=9.09658 StartZ=0 EndX=-3.75 EndY=6.49519 EndZ=0
    g35: LineSegment StartX=-3.75 StartY=6.49519 StartZ=0 EndX=-2.46335 EndY=13.9265 EndZ=0
    g36: LineSegment StartX=2.46335 StartY=13.9265 StartZ=0 EndX=3.75 EndY=6.49519 EndZ=0
    g37: LineSegment StartX=3.75 StartY=6.49519 StartZ=0 EndX=10.829 EndY=9.09658 EndZ=0
    g38: LineSegment StartX=13.2924 StartY=4.82993 StartZ=0 EndX=7.5 EndY=0 EndZ=0
    g39: LineSegment StartX=7.5 StartY=0 StartZ=0 EndX=13.2924 EndY=-4.82993 EndZ=0
    g40: LineSegment StartX=10.829 StartY=-9.09658 StartZ=0 EndX=3.75 EndY=-6.49519 EndZ=0
    g41: LineSegment StartX=3.75 StartY=-6.49519 StartZ=0 EndX=2.46335 EndY=-13.9265 EndZ=0
    g42: LineSegment StartX=-2.46335 StartY=-13.9265 StartZ=0 EndX=-3.75 EndY=-6.49519 EndZ=0
    g43: LineSegment StartX=-3.75 StartY=-6.49519 StartZ=0 EndX=-10.829 EndY=-9.09658 EndZ=0
    g44: LineSegment StartX=-13.2924 StartY=-4.82993 StartZ=0 EndX=-7.5 EndY=0 EndZ=0
    g45: LineSegment StartX=-7.5 StartY=0 StartZ=0 EndX=-13.2924 EndY=4.82993 EndZ=0
    g46: Circle CenterX=-11.6913 CenterY=6.75 CenterZ=0 NormalX=0 NormalY=0 NormalZ=1 AngleXU=0 Radius=0.75
    g47: Circle CenterX=-9.09327 CenterY=5.25 CenterZ=0 NormalX=0 NormalY=0 NormalZ=1 AngleXU=0 Radius=0.75
    g48: Circle CenterX=-6.49519 CenterY=3.75 CenterZ=0 NormalX=0 NormalY=0 NormalZ=1 AngleXU=0 Radius=0.75
    g49: Circle CenterX=0 CenterY=13.5 CenterZ=0 NormalX=0 NormalY=0 NormalZ=1 AngleXU=0 Radius=0.75
    g50: Circle CenterX=0 CenterY=10.5 CenterZ=0 NormalX=0 NormalY=0 NormalZ=1 AngleXU=0 Radius=0.75
    g51: Circle CenterX=0 CenterY=7.5 CenterZ=0 NormalX=0 NormalY=0 NormalZ=1 AngleXU=0 Radius=0.75
    g52: Circle CenterX=11.6913 CenterY=6.75 CenterZ=0 NormalX=0 NormalY=0 NormalZ=1 AngleXU=0 Radius=0.75
    g53: Circle CenterX=9.09327 CenterY=5.25 CenterZ=0 NormalX=0 NormalY=0 NormalZ=1 AngleXU=0 Radius=0.75
    g54: Circle CenterX=6.49519 CenterY=3.75 CenterZ=0 NormalX=0 NormalY=0 NormalZ=1 AngleXU=0 Radius=0.75
    g55: Circle CenterX=11.6913 CenterY=-6.75 CenterZ=0 NormalX=0 NormalY=0 NormalZ=1 AngleXU=0 Radius=0.75
    g56: Circle CenterX=9.09327 CenterY=-5.25 CenterZ=0 NormalX=0 NormalY=0 NormalZ=1 AngleXU=0 Radius=0.75
    g57: Circle CenterX=6.49519 CenterY=-3.75 CenterZ=0 NormalX=0 NormalY=0 NormalZ=1 AngleXU=0 Radius=0.75
    g58: Circle CenterX=9.8e-15 CenterY=-7.5 CenterZ=0 NormalX=0 NormalY=0 NormalZ=1 AngleXU=0 Radius=0.75
    g59: Circle CenterX=-1.42e-14 CenterY=-10.5 CenterZ=0 NormalX=0 NormalY=0 NormalZ=1 AngleXU=0 Radius=0.75
    g60: Circle CenterX=0 CenterY=-13.5 CenterZ=0 NormalX=0 NormalY=0 NormalZ=1 AngleXU=0 Radius=0.75
    g61: Circle CenterX=-11.6913 CenterY=-6.75 CenterZ=0 NormalX=0 NormalY=0 NormalZ=1 AngleXU=0 Radius=0.75
    g62: Circle CenterX=-9.09327 CenterY=-5.25 CenterZ=0 NormalX=0 NormalY=0 NormalZ=1 AngleXU=0 Radius=0.75
    g63: Circle CenterX=-6.49519 CenterY=-3.75 CenterZ=0 NormalX=0 NormalY=0 NormalZ=1 AngleXU=0 Radius=0.75
  constraints (136):
    c: Coincident(g0,g1)
    c: Coincident(g1,g2)
    c: Coincident(g2,g3)
    c: Coincident(g3,g4)
    c: Coincident(g4,g5)
    c: Coincident(g5,g0)
    c: Equal(g0, g1-g5) x5
    c: PointOnObject(g0,g6)
    c: PointOnObject(g1,g6)
    c: PointOnObject(g2,g6)
    c: PointOnObject(g3,g6)
    c: PointOnObject(g4,g6)
    c: PointOnObject(g5,g6)
    c: Coincident(g6,g-1)
    c: Coincident(g7,g8)
    c: Coincident(g8,g9)
    c: Coincident(g9,g10)
    c: Coincident(g10,g11)
    c: Coincident(g11,g12)
    c: Coincident(g12,g7)
    c: Equal(g7, g8-g12) x5
    c: PointOnObject(g7,g13)
    c: PointOnObject(g8,g13)
    c: PointOnObject(g9,g13)
    c: PointOnObject(g10,g13)
    c: PointOnObject(g11,g13)
    c: PointOnObject(g12,g13)
    c: Coincident(g13,g-1)
    c: PointOnObject(g12,g6)
    c: PointOnObject(g7,g-2)
    c: Horizontal(g5)
    c: Radius(g6) = 7.5
    c: Coincident(g14,g15)
    c: Coincident(g15,g16)
    c: Coincident(g16,g17)
    c: Coincident(g17,g18)
    c: Coincident(g18,g19)
    c: Coincident(g19,g14)
    c: Equal(g14, g15-g19) x5
    c: PointOnObject(g14,g20)
    c: PointOnObject(g15,g20)
    c: PointOnObject(g16,g20)
    c: PointOnObject(g17,g20)
    c: PointOnObject(g18,g20)
    c: PointOnObject(g19,g20)
    c: Coincident(g20,g-1)
    c: PointOnObject(g19,g-2)
    c: Radius(g20) = 10.5
    c: Coincident(g21,g22)
    c: Coincident(g22,g23)
    c: Coincident(g23,g24)
    c: Coincident(g24,g25)
    c: Coincident(g25,g26)
    c: Coincident(g26,g21)
    c: Equal(g21, g22-g26) x5
    c: PointOnObject(g21,g27)
    c: PointOnObject(g22,g27)
    c: PointOnObject(g23,g27)
    c: PointOnObject(g24,g27)
    c: PointOnObject(g25,g27)
    c: PointOnObject(g26,g27)
    c: Coincident(g27,g-1)
    c: PointOnObject(g26,g-2)
    c: Radius(g27) = 13.5
    c: Coincident(g28,g21)
    c: Coincident(g29,g25)
    c: Coincident(g30,g24)
    c: Coincident(g31,g23)
    c: Coincident(g32,g22)
    c: Coincident(g33,g21)
    c: Coincident(g34,g0)
    c: Coincident(g35,g34)
    c: Coincident(g36,g4)
    c: Coincident(g37,g36)
    c: Coincident(g38,g3)
    c: Coincident(g39,g38)
    c: Coincident(g40,g2)
    c: Coincident(g41,g40)
    c: Coincident(g42,g1)
    c: Coincident(g43,g42)
    c: Coincident(g44,g0)
    c: Coincident(g45,g44)
    c: Tangent(g35,g28) = 1.5708
    c: Tangent(g36,g28) = 1.5708
    c: Tangent(g37,g29) = 1.5708
    c: Tangent(g38,g29) = 1.5708
    c: Tangent(g39,g30) = 1.5708
    c: Tangent(g40,g30) = 1.5708
    c: Tangent(g41,g31) = 1.5708
    c: Tangent(g42,g31) = 1.5708
    c: Tangent(g43,g32) = 1.5708
    c: Tangent(g44,g32) = 1.5708
    c: Tangent(g45,g33) = 1.5708
    c: Tangent(g34,g33) = 1.5708
    c: Radius(g29) = 2.5
    c: Equal(g29,g28)
    c: Equal(g28,g33)
    c: Equal(g33,g32)
    c: Equal(g32,g31)
    c: Equal(g31,g30)
    c: Coincident(g46,g33)
    c: Coincident(g47,g14)
    c: Coincident(g48,g7)
    c: Coincident(g49,g28)
    c: Coincident(g50,g14)
    c: Coincident(g51,g7)
    c: Coincident(g52,g29)
    c: Coincident(g53,g18)
    c: Coincident(g54,g11)
    c: Coincident(g55,g30)
    c: Coincident(g56,g17)
    c: Coincident(g57,g10)
    c: Coincident(g58,g9)
    c: Coincident(g59,g16)
    c: Coincident(g60,g31)
    c: Coincident(g61,g32)
    c: Coincident(g62,g15)
    c: Coincident(g63,g8)
    c: Equal(g61,g62)
    c: Equal(g62,g63)
    c: Equal(g63,g58)
    c: Equal(g58,g59)
    c: Equal(g59,g60)
    c: Equal(g60,g55)
    c: Equal(g55,g56)
    c: Equal(g56,g57)
    c: Equal(g57,g54)
    c: Equal(g54,g53)
    c: Equal(g53,g52)
    c: Equal(g52,g51)
    c: Equal(g51,g50)
    c: Equal(g50,g49)
    c: Equal(g49,g46)
    c: Equal(g46,g47)
    c: Equal(g47,g48)
    c: Radius(g55) = 0.75
FEATURE [PartDesign::Pad] Pad923
  Length = 2
  Length2 = 100
  Profile = -> Sketch2143
  Type = 0
FEATURE [Sketcher::SketchObject] Sketch2141
  MapMode = 5
  Placement = pos=(0,0,2) rot=(0,0,1;0rad)
  Support = -> [Pad923]
  sketch-geometry (2):
    g0: Circle CenterX=0 CenterY=0 CenterZ=0 NormalX=0 NormalY=0 NormalZ=1 AngleXU=0 Radius=5
    g1: Circle CenterX=0 CenterY=0 CenterZ=0 NormalX=0 NormalY=0 NormalZ=1 AngleXU=0 Radius=3.5
  constraints (4):
    c: Coincident(g0,g-1)
    c: Coincident(g1,g0)
    c: Radius(g1) = 3.5
    c: Radius(g0) = 5
FEATURE [PartDesign::Pocket] Pocket755
  BaseFeature = -> Pad923
  Length = 1
  Length2 = 100
  Profile = -> Sketch2141
  Type = 0
FEATURE [Sketcher::SketchObject] Sketch2140
  MapMode = 5
  Placement = pos=(0,0,2) rot=(0,0,1;0rad)
  Support = -> [Pocket755]
  sketch-geometry (1):
    g0: Circle CenterX=0 CenterY=0 CenterZ=0 NormalX=0 NormalY=0 NormalZ=1 AngleXU=0 Radius=3
  constraints (2):
    c: Coincident(g0,g-1)
    c: Radius(g0) = 3
FEATURE [PartDesign::Pocket] Pocket759
  BaseFeature = -> Pocket755
  Length = 1
  Length2 = 100
  Profile = -> Sketch2140
  Type = 0
FEATURE [Sketcher::SketchObject] Sketch2142
  MapMode = 5
  Placement = pos=(0,0,1) rot=(0,0,1;0rad)
  Support = -> [Pocket759]
  sketch-geometry (1):
    g0: Circle CenterX=0 CenterY=0 CenterZ=0 NormalX=0 NormalY=0 NormalZ=1 AngleXU=0 Radius=1.5
  constraints (2):
    c: Coincident(g0,g-1)
    c: Radius(g0) = 1.5
FEATURE [PartDesign::Pocket] Pocket756
  BaseFeature = -> Pocket759
  Length = 5
  Length2 = 100
  Profile = -> Sketch2142
  Type = 0
FEATURE [Sketcher::SketchObject] Sketch2144
  MapMode = 5
  Placement = pos=(0,0,0) rot=(1,0,0;3.14159rad)
  Support = -> [Pocket756]
  sketch-geometry (2):
    g0: Circle CenterX=0 CenterY=0 CenterZ=0 NormalX=0 NormalY=0 NormalZ=1 AngleXU=0 Radius=4.5
    g1: Circle CenterX=0 CenterY=0 CenterZ=0 NormalX=0 NormalY=0 NormalZ=1 AngleXU=0 Radius=3
  constraints (4):
    c: Coincident(g0,g-1)
    c: Coincident(g1,g0)
    c: Radius(g0) = 4.5
    c: Radius(g1) = 3
FEATURE [PartDesign::Pad] Pad919
  BaseFeature = -> Pocket756
  Length = 3
  Length2 = 100
  Profile = -> Sketch2144
  Type = 0
FEATURE [PartDesign::Fillet] Fillet251
  Base = -> Pad919 [Face5,Edge96,Face4]
  BaseFeature = -> Pad919
  Radius = 0.2
FEATURE [PartDesign::Body] Body585  label="M2x087"
  Group = -> [Sketch2102,Pad920,Sketch2098,Pad926,Sketch2103,Pocket761,Chamfer445]
  Origin = -> Origin842
  Tip = -> Chamfer445
FEATURE [PartDesign::Body] Body586  label="Futuba FSH6B011"
  Group = -> [Sketch2143,Pad923,Sketch2141,Pocket755,Sketch2140,Pocket759,Sketch2142,Pocket756,Sketch2144,Pad919,Fillet251]
  Origin = -> Origin828
  Tip = -> Fillet251
FEATURE [App::Part] Part235  label="Servohorn018"
  Group = -> [Body586]
  Origin = -> Origin831
  Placement = pos=(0,0,-67) rot=(0,0,1;0rad)
FEATURE [PartDesign::Body] Body587  label="M2 Nut076"
  Group = -> [Sketch2105,Pad932,Sketch2101,Groove196,Chamfer444,Sketch2100,Sketch2099]
  Origin = -> Origin846
  Placement = pos=(0,0,2.75) rot=(0,0,1;0rad)
  Tip = -> Chamfer444
FEATURE [App::Part] Part239  label="M075"
  Group = -> [Body585,Body587]
  Origin = -> Origin844
  Placement = pos=(-9.8e-15,10.5,80) rot=(0,1,0;3.14159rad)
FEATURE [PartDesign::Body] Body588  label="M2x088"
  Group = -> [Sketch2107,Pad931,Sketch2122,Pad933,Sketch2123,Pocket757,Chamfer447]
  Origin = -> Origin835
  Tip = -> Chamfer447
FEATURE [PartDesign::Body] Body589  label="M2x089"
  Group = -> [Sketch2108,Pad924,Sketch2117,Pad927,Sketch2124,Pocket762,Chamfer443]
  Origin = -> Origin827
  Tip = -> Chamfer443
FEATURE [PartDesign::Body] Body590  label="M2 Nut077"
  Group = -> [Sketch2125,Pad925,Sketch2111,Groove197,Chamfer438,Sketch2110,Sketch2114]
  Origin = -> Origin825
  Placement = pos=(0,0,2.75) rot=(0,0,1;0rad)
  Tip = -> Chamfer438
FEATURE [App::Part] Part240  label="M076"
  Group = -> [Body588,Body590]
  Origin = -> Origin840
  Placement = pos=(-9.8e-15,-10.5,80) rot=(0,1,0;3.14159rad)
FEATURE [PartDesign::Body] Body591  label="M2 Nut078"
  Group = -> [Sketch2104,Pad930,Sketch2118,Groove194,Chamfer437,Sketch2116,Sketch2106]
  Origin = -> Origin837
  Placement = pos=(0,0,2.75) rot=(0,0,1;0rad)
  Tip = -> Chamfer437
FEATURE [App::Part] Part237  label="M074"
  Group = -> [Body589,Body591]
  Origin = -> Origin829
  Placement = pos=(-9.1,-5.25,80) rot=(0,1,0;3.14159rad)
FEATURE [PartDesign::Body] Body592  label="M2 Nut079"
  Group = -> [Sketch2109,Pad935,Sketch2129,Groove193,Chamfer446,Sketch2139,Sketch2127]
  Origin = -> Origin836
  Placement = pos=(0,0,2.75) rot=(0,0,1;0rad)
  Tip = -> Chamfer446
FEATURE [PartDesign::Body] Body593  label="M2 Nut080"
  Group = -> [Sketch2128,Pad938,Sketch2134,Groove198,Chamfer440,Sketch2132,Sketch2135]
  Origin = -> Origin833
  Placement = pos=(0,0,2.75) rot=(0,0,1;0rad)
  Tip = -> Chamfer440
FEATURE [PartDesign::Body] Body594  label="M2x090"
  Group = -> [Sketch2138,Pad922,Sketch2137,Pad921,Sketch2119,Pocket758,Chamfer442]
  Origin = -> Origin834
  Tip = -> Chamfer442
FEATURE [App::Part] Part243  label="M079"
  Group = -> [Body594,Body593]
  Origin = -> Origin826
  Placement = pos=(-9.1,5.25,80) rot=(0,1,0;3.14159rad)
FEATURE [PartDesign::Body] Body595  label="M2 Nut081"
  Group = -> [Sketch2115,Pad936,Sketch2126,Groove195,Chamfer436,Sketch2130,Sketch2136]
  Origin = -> Origin843
  Placement = pos=(0,0,2.75) rot=(0,0,1;0rad)
  Tip = -> Chamfer436
FEATURE [PartDesign::Body] Body596  label="M2x091"
  Group = -> [Sketch2121,Pad928,Sketch2131,Pad937,Sketch2133,Pocket763,Chamfer441]
  Origin = -> Origin845
  Tip = -> Chamfer441
FEATURE [App::Part] Part241  label="M077"
  Group = -> [Body596,Body595]
  Origin = -> Origin841
  Placement = pos=(9.1,5.25,80) rot=(0,1,0;3.14159rad)
FEATURE [PartDesign::Body] Body597  label="M2x092"
  Group = -> [Sketch2112,Pad929,Sketch2120,Pad934,Sketch2113,Pocket760,Chamfer439]
  Origin = -> Origin838
  Tip = -> Chamfer439
FEATURE [App::Part] Part242  label="M078"
  Group = -> [Body597,Body592]
  Origin = -> Origin830
  Placement = pos=(9.1,-5.25,80) rot=(0,1,0;3.14159rad)
FEATURE [App::Part] Part238  label="Screws016"
  Group = -> [Part239,Part240,Part237,Part242,Part241,Part243]
  Origin = -> Origin832
  Placement = pos=(0,0,-141) rot=(0,0,1;0rad)
FEATURE [Sketcher::SketchObject] Sketch2247
  MapMode = 5
  Support = -> [XY_Plane892]
  sketch-geometry (1):
    g0: Circle CenterX=0 CenterY=0 CenterZ=0 NormalX=0 NormalY=0 NormalZ=1 AngleXU=0 Radius=2.75
  constraints (2):
    c: Coincident(g0,g-1)
    c: Radius(g0) = 2.75
FEATURE [PartDesign::Pad] Pad980  label="M3x8 Head137"
  Length = 3
  Length2 = 100
  Profile = -> Sketch2247
  Type = 0
FEATURE [Sketcher::SketchObject] Sketch2248
  MapMode = 5
  Placement = pos=(0,0,3) rot=(0,0,1;0rad)
  Support = -> [Pad980]
  sketch-geometry (1):
    g0: Circle CenterX=0 CenterY=0 CenterZ=0 NormalX=0 NormalY=0 NormalZ=1 AngleXU=0 Radius=1.5
  constraints (2):
    c: Coincident(g0,g-1)
    c: Radius(g0) = 1.5
FEATURE [PartDesign::Pad] Pad981  label="M3x8 Thread137"
  BaseFeature = -> Pad980
  Length = 8
  Length2 = 100
  Profile = -> Sketch2248
  Type = 0
FEATURE [Sketcher::SketchObject] Sketch2246
  MapMode = 5
  Placement = pos=(0,0,0) rot=(1,0,0;3.14159rad)
  Support = -> [Pad981]
  sketch-geometry (7):
    g0: LineSegment StartX=1.275 StartY=0.736122 StartZ=0 EndX=0 EndY=1.47224 EndZ=0
    g1: LineSegment StartX=0 StartY=1.47224 StartZ=0 EndX=-1.275 EndY=0.736122 EndZ=0
    g2: LineSegment StartX=-1.275 StartY=0.736122 StartZ=0 EndX=-1.275 EndY=-0.736122 EndZ=0
    g3: LineSegment StartX=-1.275 StartY=-0.736122 StartZ=0 EndX=1.34766e-11 EndY=-1.47224 EndZ=0
    g4: LineSegment StartX=1.34766e-11 StartY=-1.47224 StartZ=0 EndX=1.275 EndY=-0.736122 EndZ=0
    g5: LineSegment StartX=1.275 StartY=-0.736122 StartZ=0 EndX=1.275 EndY=0.736122 EndZ=0
    g6: Circle [constr] CenterX=0 CenterY=0 CenterZ=0 NormalX=0 NormalY=0 NormalZ=1 AngleXU=0 Radius=1.47224
  constraints (16):
    c: Coincident(g0,g1)
    c: Coincident(g1,g2)
    c: Coincident(g2,g3)
    c: Coincident(g3,g4)
    c: Coincident(g4,g5)
    c: Coincident(g5,g0)
    c: Equal(g0, g1-g5) x5
    c: PointOnObject(g0,g6)
    c: PointOnObject(g1,g6)
    c: PointOnObject(g2,g6)
    c: PointOnObject(g3,g6)
    c: PointOnObject(g4,g6)
    c: PointOnObject(g5,g6)
    c: Coincident(g6,g-1)
    c: PointOnObject(g0,g-2)
    c: DistanceX(g1,g0) = 2.55
FEATURE [PartDesign::Pocket] Pocket788  label="M3x8 Wrench137"
  BaseFeature = -> Pad981
  Length = 1.3
  Length2 = 100
  Profile = -> Sketch2246
  Type = 0
FEATURE [PartDesign::Chamfer] Chamfer472  label="M3x8 Smooth136"
  Base = -> Pocket788 [Face11,Edge2,Edge24,Edge3]
  BaseFeature = -> Pocket788
  Size = 0.2
FEATURE [PartDesign::Body] Body625  label="FOS Servohorn Left M3x8"
  Group = -> [Sketch2247,Pad980,Sketch2248,Pad981,Sketch2246,Pocket788,Chamfer472]
  Origin = -> Origin894
  Placement = pos=(8e-15,0,-63) rot=(0,1,0;3.14159rad)
  Tip = -> Chamfer472
FEATURE [App::Part] Part234  label="FOS Servohorn Left"
  Group = -> [Part226,Part228,Body625]
  Origin = -> Origin824
  Placement = pos=(184.85,-60.65,210.6) rot=(-0.57735,-0.57735,-0.57735;4.18879rad)
FEATURE [Sketcher::SketchObject] Sketch2250
  MapMode = 5
  Support = -> [XY_Plane893]
  sketch-geometry (1):
    g0: Circle CenterX=0 CenterY=0 CenterZ=0 NormalX=0 NormalY=0 NormalZ=1 AngleXU=0 Radius=2.75
  constraints (2):
    c: Coincident(g0,g-1)
    c: Radius(g0) = 2.75
FEATURE [PartDesign::Pad] Pad982  label="M3x8 Head138"
  Length = 3
  Length2 = 100
  Profile = -> Sketch2250
  Type = 0
FEATURE [Sketcher::SketchObject] Sketch2251
  MapMode = 5
  Placement = pos=(0,0,3) rot=(0,0,1;0rad)
  Support = -> [Pad982]
  sketch-geometry (1):
    g0: Circle CenterX=0 CenterY=0 CenterZ=0 NormalX=0 NormalY=0 NormalZ=1 AngleXU=0 Radius=1.5
  constraints (2):
    c: Coincident(g0,g-1)
    c: Radius(g0) = 1.5
FEATURE [PartDesign::Pad] Pad983  label="M3x8 Thread138"
  BaseFeature = -> Pad982
  Length = 8
  Length2 = 100
  Profile = -> Sketch2251
  Type = 0
FEATURE [Sketcher::SketchObject] Sketch2249
  MapMode = 5
  Placement = pos=(0,0,0) rot=(1,0,0;3.14159rad)
  Support = -> [Pad983]
  sketch-geometry (7):
    g0: LineSegment StartX=1.275 StartY=0.736122 StartZ=0 EndX=0 EndY=1.47224 EndZ=0
    g1: LineSegment StartX=0 StartY=1.47224 StartZ=0 EndX=-1.275 EndY=0.736122 EndZ=0
    g2: LineSegment StartX=-1.275 StartY=0.736122 StartZ=0 EndX=-1.275 EndY=-0.736122 EndZ=0
    g3: LineSegment StartX=-1.275 StartY=-0.736122 StartZ=0 EndX=1.34766e-11 EndY=-1.47224 EndZ=0
    g4: LineSegment StartX=1.34766e-11 StartY=-1.47224 StartZ=0 EndX=1.275 EndY=-0.736122 EndZ=0
    g5: LineSegment StartX=1.275 StartY=-0.736122 StartZ=0 EndX=1.275 EndY=0.736122 EndZ=0
    g6: Circle [constr] CenterX=0 CenterY=0 CenterZ=0 NormalX=0 NormalY=0 NormalZ=1 AngleXU=0 Radius=1.47224
  constraints (16):
    c: Coincident(g0,g1)
    c: Coincident(g1,g2)
    c: Coincident(g2,g3)
    c: Coincident(g3,g4)
    c: Coincident(g4,g5)
    c: Coincident(g5,g0)
    c: Equal(g0, g1-g5) x5
    c: PointOnObject(g0,g6)
    c: PointOnObject(g1,g6)
    c: PointOnObject(g2,g6)
    c: PointOnObject(g3,g6)
    c: PointOnObject(g4,g6)
    c: PointOnObject(g5,g6)
    c: Coincident(g6,g-1)
    c: PointOnObject(g0,g-2)
    c: DistanceX(g1,g0) = 2.55
FEATURE [PartDesign::Pocket] Pocket789  label="M3x8 Wrench138"
  BaseFeature = -> Pad983
  Length = 1.3
  Length2 = 100
  Profile = -> Sketch2249
  Type = 0
FEATURE [PartDesign::Chamfer] Chamfer473  label="M3x8 Smooth137"
  Base = -> Pocket789 [Face11,Edge2,Edge24,Edge3]
  BaseFeature = -> Pocket789
  Size = 0.2
FEATURE [PartDesign::Body] Body626  label="FOS Servohorn Right M3x8"
  Group = -> [Sketch2250,Pad982,Sketch2251,Pad983,Sketch2249,Pocket789,Chamfer473]
  Origin = -> Origin895
  Placement = pos=(0,0,-63) rot=(0,1,0;3.14159rad)
  Tip = -> Chamfer473
FEATURE [App::Part] Part236  label="FOS Servohorn Right"
  Group = -> [Part235,Part238,Body626]
  Origin = -> Origin839
  Placement = pos=(184.9,-138.65,210.65) rot=(0.57735,0.57735,0.57735;2.0944rad)
FEATURE [App::Part] Part225  label="Front Outer Shoulder"
  Group = -> [Body,Part234,Part236]
  Origin = -> Origin802
FEATURE [App::Part] Part223  label="Front Shoulder"
  Group = -> [Part225]
  Origin = -> Origin800
  Placement = pos=(-95.25,0,0) rot=(0,0,1;0rad)
FEATURE [Sketcher::SketchObject] Sketch2252
  MapMode = 5
  Support = -> [XY_Plane932]
FEATURE [Sketcher::SketchObject] Sketch2253
  MapMode = 5
  Support = -> [XY_Plane901]
FEATURE [Sketcher::SketchObject] Sketch2255
  MapMode = 5
  Support = -> [XY_Plane898]
FEATURE [Sketcher::SketchObject] Sketch2256
  MapMode = 5
  Support = -> [XY_Plane935]
  sketch-geometry (64):
    g0: LineSegment [constr] StartX=-3.75 StartY=6.49519 StartZ=0 EndX=-7.5 EndY=0 EndZ=0
    g1: LineSegment [constr] StartX=-7.5 StartY=0 StartZ=0 EndX=-3.75 EndY=-6.49519 EndZ=0
    g2: LineSegment [constr] StartX=-3.75 StartY=-6.49519 StartZ=0 EndX=3.75 EndY=-6.49519 EndZ=0
    g3: LineSegment [constr] StartX=3.75 StartY=-6.49519 StartZ=0 EndX=7.5 EndY=0 EndZ=0
    g4: LineSegment [constr] StartX=7.5 StartY=0 StartZ=0 EndX=3.75 EndY=6.49519 EndZ=0
    g5: LineSegment [constr] StartX=3.75 StartY=6.49519 StartZ=0 EndX=-3.75 EndY=6.49519 EndZ=0
    g6: Circle [constr] CenterX=0 CenterY=0 CenterZ=0 NormalX=0 NormalY=0 NormalZ=1 AngleXU=0 Radius=7.5
    g7: LineSegment [constr] StartX=0 StartY=7.5 StartZ=0 EndX=-6.49519 EndY=3.75 EndZ=0
    g8: LineSegment [constr] StartX=-6.49519 StartY=3.75 StartZ=0 EndX=-6.49519 EndY=-3.75 EndZ=0
    g9: LineSegment [constr] StartX=-6.49519 StartY=-3.75 StartZ=0 EndX=9.8e-15 EndY=-7.5 EndZ=0
    g10: LineSegment [constr] StartX=9.8e-15 StartY=-7.5 StartZ=0 EndX=6.49519 EndY=-3.75 EndZ=0
    g11: LineSegment [constr] StartX=6.49519 StartY=-3.75 StartZ=0 EndX=6.49519 EndY=3.75 EndZ=0
    g12: LineSegment [constr] StartX=6.49519 StartY=3.75 StartZ=0 EndX=0 EndY=7.5 EndZ=0
    g13: Circle [constr] CenterX=0 CenterY=0 CenterZ=0 NormalX=0 NormalY=0 NormalZ=1 AngleXU=0 Radius=7.5
    g14: LineSegment [constr] StartX=0 StartY=10.5 StartZ=0 EndX=-9.09327 EndY=5.25 EndZ=0
    g15: LineSegment [constr] StartX=-9.09327 StartY=5.25 StartZ=0 EndX=-9.09327 EndY=-5.25 EndZ=0
    g16: LineSegment [constr] StartX=-9.09327 StartY=-5.25 StartZ=0 EndX=-1.42e-14 EndY=-10.5 EndZ=0
    g17: LineSegment [constr] StartX=-1.42e-14 StartY=-10.5 StartZ=0 EndX=9.09327 EndY=-5.25 EndZ=0
    g18: LineSegment [constr] StartX=9.09327 StartY=-5.25 StartZ=0 EndX=9.09327 EndY=5.25 EndZ=0
    g19: LineSegment [constr] StartX=9.09327 StartY=5.25 StartZ=0 EndX=0 EndY=10.5 EndZ=0
    g20: Circle [constr] CenterX=0 CenterY=0 CenterZ=0 NormalX=0 NormalY=0 NormalZ=1 AngleXU=0 Radius=10.5
    g21: LineSegment [constr] StartX=0 StartY=13.5 StartZ=0 EndX=-11.6913 EndY=6.75 EndZ=0
    g22: LineSegment [constr] StartX=-11.6913 StartY=6.75 StartZ=0 EndX=-11.6913 EndY=-6.75 EndZ=0
    g23: LineSegment [constr] StartX=-11.6913 StartY=-6.75 StartZ=0 EndX=0 EndY=-13.5 EndZ=0
    g24: LineSegment [constr] StartX=0 StartY=-13.5 StartZ=0 EndX=11.6913 EndY=-6.75 EndZ=0
    g25: LineSegment [constr] StartX=11.6913 StartY=-6.75 StartZ=0 EndX=11.6913 EndY=6.75 EndZ=0
    g26: LineSegment [constr] StartX=11.6913 StartY=6.75 StartZ=0 EndX=0 EndY=13.5 EndZ=0
    g27: Circle [constr] CenterX=0 CenterY=0 CenterZ=0 NormalX=0 NormalY=0 NormalZ=1 AngleXU=0 Radius=13.5
    g28: ArcOfCircle CenterX=0 CenterY=13.5 CenterZ=0 NormalX=0 NormalY=0 NormalZ=1 AngleXU=0 Radius=2.5 StartAngle=0.171439 EndAngle=2.97015
    g29: ArcOfCircle CenterX=11.6913 CenterY=6.75 CenterZ=0 NormalX=0 NormalY=0 NormalZ=1 AngleXU=0 Radius=2.5 StartAngle=5.40743 EndAngle=8.20614
    g30: ArcOfCircle CenterX=11.6913 CenterY=-6.75 CenterZ=0 NormalX=0 NormalY=0 NormalZ=1 AngleXU=0 Radius=2.5 StartAngle=4.36023 EndAngle=7.15894
    g31: ArcOfCircle CenterX=0 CenterY=-13.5 CenterZ=0 NormalX=0 NormalY=0 NormalZ=1 AngleXU=0 Radius=2.5 StartAngle=3.31303 EndAngle=6.11175
    g32: ArcOfCircle CenterX=-11.6913 CenterY=-6.75 CenterZ=0 NormalX=0 NormalY=0 NormalZ=1 AngleXU=0 Radius=2.5 StartAngle=2.26583 EndAngle=5.06455
    g33: ArcOfCircle CenterX=-11.6913 CenterY=6.75 CenterZ=0 NormalX=0 NormalY=0 NormalZ=1 AngleXU=0 Radius=2.5 StartAngle=1.21864 EndAngle=4.01735
    g34: LineSegment StartX=-10.829 StartY=9.09658 StartZ=0 EndX=-3.75 EndY=6.49519 EndZ=0
    g35: LineSegment StartX=-3.75 StartY=6.49519 StartZ=0 EndX=-2.46335 EndY=13.9265 EndZ=0
    g36: LineSegment StartX=2.46335 StartY=13.9265 StartZ=0 EndX=3.75 EndY=6.49519 EndZ=0
    g37: LineSegment StartX=3.75 StartY=6.49519 StartZ=0 EndX=10.829 EndY=9.09658 EndZ=0
    g38: LineSegment StartX=13.2924 StartY=4.82993 StartZ=0 EndX=7.5 EndY=0 EndZ=0
    g39: LineSegment StartX=7.5 StartY=0 StartZ=0 EndX=13.2924 EndY=-4.82993 EndZ=0
    g40: LineSegment StartX=10.829 StartY=-9.09658 StartZ=0 EndX=3.75 EndY=-6.49519 EndZ=0
    g41: LineSegment StartX=3.75 StartY=-6.49519 StartZ=0 EndX=2.46335 EndY=-13.9265 EndZ=0
    g42: LineSegment StartX=-2.46335 StartY=-13.9265 StartZ=0 EndX=-3.75 EndY=-6.49519 EndZ=0
    g43: LineSegment StartX=-3.75 StartY=-6.49519 StartZ=0 EndX=-10.829 EndY=-9.09658 EndZ=0
    g44: LineSegment StartX=-13.2924 StartY=-4.82993 StartZ=0 EndX=-7.5 EndY=0 EndZ=0
    g45: LineSegment StartX=-7.5 StartY=0 StartZ=0 EndX=-13.2924 EndY=4.82993 EndZ=0
    g46: Circle CenterX=-11.6913 CenterY=6.75 CenterZ=0 NormalX=0 NormalY=0 NormalZ=1 AngleXU=0 Radius=0.75
    g47: Circle CenterX=-9.09327 CenterY=5.25 CenterZ=0 NormalX=0 NormalY=0 NormalZ=1 AngleXU=0 Radius=0.75
    g48: Circle CenterX=-6.49519 CenterY=3.75 CenterZ=0 NormalX=0 NormalY=0 NormalZ=1 AngleXU=0 Radius=0.75
    g49: Circle CenterX=0 CenterY=13.5 CenterZ=0 NormalX=0 NormalY=0 NormalZ=1 AngleXU=0 Radius=0.75
    g50: Circle CenterX=0 CenterY=10.5 CenterZ=0 NormalX=0 NormalY=0 NormalZ=1 AngleXU=0 Radius=0.75
    g51: Circle CenterX=0 CenterY=7.5 CenterZ=0 NormalX=0 NormalY=0 NormalZ=1 AngleXU=0 Radius=0.75
    g52: Circle CenterX=11.6913 CenterY=6.75 CenterZ=0 NormalX=0 NormalY=0 NormalZ=1 AngleXU=0 Radius=0.75
    g53: Circle CenterX=9.09327 CenterY=5.25 CenterZ=0 NormalX=0 NormalY=0 NormalZ=1 AngleXU=0 Radius=0.75
    g54: Circle CenterX=6.49519 CenterY=3.75 CenterZ=0 NormalX=0 NormalY=0 NormalZ=1 AngleXU=0 Radius=0.75
    g55: Circle CenterX=11.6913 CenterY=-6.75 CenterZ=0 NormalX=0 NormalY=0 NormalZ=1 AngleXU=0 Radius=0.75
    g56: Circle CenterX=9.09327 CenterY=-5.25 CenterZ=0 NormalX=0 NormalY=0 NormalZ=1 AngleXU=0 Radius=0.75
    g57: Circle CenterX=6.49519 CenterY=-3.75 CenterZ=0 NormalX=0 NormalY=0 NormalZ=1 AngleXU=0 Radius=0.75
    g58: Circle CenterX=9.8e-15 CenterY=-7.5 CenterZ=0 NormalX=0 NormalY=0 NormalZ=1 AngleXU=0 Radius=0.75
    g59: Circle CenterX=-1.42e-14 CenterY=-10.5 CenterZ=0 NormalX=0 NormalY=0 NormalZ=1 AngleXU=0 Radius=0.75
    g60: Circle CenterX=0 CenterY=-13.5 CenterZ=0 NormalX=0 NormalY=0 NormalZ=1 AngleXU=0 Radius=0.75
    g61: Circle CenterX=-11.6913 CenterY=-6.75 CenterZ=0 NormalX=0 NormalY=0 NormalZ=1 AngleXU=0 Radius=0.75
    g62: Circle CenterX=-9.09327 CenterY=-5.25 CenterZ=0 NormalX=0 NormalY=0 NormalZ=1 AngleXU=0 Radius=0.75
    g63: Circle CenterX=-6.49519 CenterY=-3.75 CenterZ=0 NormalX=0 NormalY=0 NormalZ=1 AngleXU=0 Radius=0.75
  constraints (136):
    c: Coincident(g0,g1)
    c: Coincident(g1,g2)
    c: Coincident(g2,g3)
    c: Coincident(g3,g4)
    c: Coincident(g4,g5)
    c: Coincident(g5,g0)
    c: Equal(g0, g1-g5) x5
    c: PointOnObject(g0,g6)
    c: PointOnObject(g1,g6)
    c: PointOnObject(g2,g6)
    c: PointOnObject(g3,g6)
    c: PointOnObject(g4,g6)
    c: PointOnObject(g5,g6)
    c: Coincident(g6,g-1)
    c: Coincident(g7,g8)
    c: Coincident(g8,g9)
    c: Coincident(g9,g10)
    c: Coincident(g10,g11)
    c: Coincident(g11,g12)
    c: Coincident(g12,g7)
    c: Equal(g7, g8-g12) x5
    c: PointOnObject(g7,g13)
    c: PointOnObject(g8,g13)
    c: PointOnObject(g9,g13)
    c: PointOnObject(g10,g13)
    c: PointOnObject(g11,g13)
    c: PointOnObject(g12,g13)
    c: Coincident(g13,g-1)
    c: PointOnObject(g12,g6)
    c: PointOnObject(g7,g-2)
    c: Horizontal(g5)
    c: Radius(g6) = 7.5
    c: Coincident(g14,g15)
    c: Coincident(g15,g16)
    c: Coincident(g16,g17)
    c: Coincident(g17,g18)
    c: Coincident(g18,g19)
    c: Coincident(g19,g14)
    c: Equal(g14, g15-g19) x5
    c: PointOnObject(g14,g20)
    c: PointOnObject(g15,g20)
    c: PointOnObject(g16,g20)
    c: PointOnObject(g17,g20)
    c: PointOnObject(g18,g20)
    c: PointOnObject(g19,g20)
    c: Coincident(g20,g-1)
    c: PointOnObject(g19,g-2)
    c: Radius(g20) = 10.5
    c: Coincident(g21,g22)
    c: Coincident(g22,g23)
    c: Coincident(g23,g24)
    c: Coincident(g24,g25)
    c: Coincident(g25,g26)
    c: Coincident(g26,g21)
    c: Equal(g21, g22-g26) x5
    c: PointOnObject(g21,g27)
    c: PointOnObject(g22,g27)
    c: PointOnObject(g23,g27)
    c: PointOnObject(g24,g27)
    c: PointOnObject(g25,g27)
    c: PointOnObject(g26,g27)
    c: Coincident(g27,g-1)
    c: PointOnObject(g26,g-2)
    c: Radius(g27) = 13.5
    c: Coincident(g28,g21)
    c: Coincident(g29,g25)
    c: Coincident(g30,g24)
    c: Coincident(g31,g23)
    c: Coincident(g32,g22)
    c: Coincident(g33,g21)
    c: Coincident(g34,g0)
    c: Coincident(g35,g34)
    c: Coincident(g36,g4)
    c: Coincident(g37,g36)
    c: Coincident(g38,g3)
    c: Coincident(g39,g38)
    c: Coincident(g40,g2)
    c: Coincident(g41,g40)
    c: Coincident(g42,g1)
    c: Coincident(g43,g42)
    c: Coincident(g44,g0)
    c: Coincident(g45,g44)
    c: Tangent(g35,g28) = 1.5708
    c: Tangent(g36,g28) = 1.5708
    c: Tangent(g37,g29) = 1.5708
    c: Tangent(g38,g29) = 1.5708
    c: Tangent(g39,g30) = 1.5708
    c: Tangent(g40,g30) = 1.5708
    c: Tangent(g41,g31) = 1.5708
    c: Tangent(g42,g31) = 1.5708
    c: Tangent(g43,g32) = 1.5708
    c: Tangent(g44,g32) = 1.5708
    c: Tangent(g45,g33) = 1.5708
    c: Tangent(g34,g33) = 1.5708
    c: Radius(g29) = 2.5
    c: Equal(g29,g28)
    c: Equal(g28,g33)
    c: Equal(g33,g32)
    c: Equal(g32,g31)
    c: Equal(g31,g30)
    c: Coincident(g46,g33)
    c: Coincident(g47,g14)
    c: Coincident(g48,g7)
    c: Coincident(g49,g28)
    c: Coincident(g50,g14)
    c: Coincident(g51,g7)
    c: Coincident(g52,g29)
    c: Coincident(g53,g18)
    c: Coincident(g54,g11)
    c: Coincident(g55,g30)
    c: Coincident(g56,g17)
    c: Coincident(g57,g10)
    c: Coincident(g58,g9)
    c: Coincident(g59,g16)
    c: Coincident(g60,g31)
    c: Coincident(g61,g32)
    c: Coincident(g62,g15)
    c: Coincident(g63,g8)
    c: Equal(g61,g62)
    c: Equal(g62,g63)
    c: Equal(g63,g58)
    c: Equal(g58,g59)
    c: Equal(g59,g60)
    c: Equal(g60,g55)
    c: Equal(g55,g56)
    c: Equal(g56,g57)
    c: Equal(g57,g54)
    c: Equal(g54,g53)
    c: Equal(g53,g52)
    c: Equal(g52,g51)
    c: Equal(g51,g50)
    c: Equal(g50,g49)
    c: Equal(g49,g46)
    c: Equal(g46,g47)
    c: Equal(g47,g48)
    c: Radius(g55) = 0.75
FEATURE [Sketcher::SketchObject] Sketch2261
  MapMode = 5
  Support = -> [XY_Plane904]
  sketch-geometry (1):
    g0: Circle CenterX=0 CenterY=0 CenterZ=0 NormalX=0 NormalY=0 NormalZ=1 AngleXU=0 Radius=1.9
  constraints (2):
    c: Coincident(g0,g-1)
    c: Radius(g0) = 1.9
FEATURE [Sketcher::SketchObject] Sketch2264
  MapMode = 5
  Support = -> [XY_Plane933]
FEATURE [Sketcher::SketchObject] Sketch2265
  MapMode = 5
  Support = -> [XY_Plane926]
FEATURE [Sketcher::SketchObject] Sketch2266
  MapMode = 5
  Support = -> [XY_Plane901]
  sketch-geometry (8):
    g0: LineSegment StartX=0 StartY=2.3094 StartZ=0 EndX=-2 EndY=1.1547 EndZ=0
    g1: LineSegment StartX=-2 StartY=1.1547 StartZ=0 EndX=-2 EndY=-1.1547 EndZ=0
    g2: LineSegment StartX=-2 StartY=-1.1547 StartZ=0 EndX=-2e-16 EndY=-2.3094 EndZ=0
    g3: LineSegment StartX=-2e-16 StartY=-2.3094 StartZ=0 EndX=2 EndY=-1.1547 EndZ=0
    g4: LineSegment StartX=2 StartY=-1.1547 StartZ=0 EndX=2 EndY=1.1547 EndZ=0
    g5: LineSegment StartX=2 StartY=1.1547 StartZ=0 EndX=0 EndY=2.3094 EndZ=0
    g6: Circle [constr] CenterX=0 CenterY=0 CenterZ=0 NormalX=0 NormalY=0 NormalZ=1 AngleXU=0 Radius=2.3094
    g7: Circle CenterX=0 CenterY=0 CenterZ=0 NormalX=0 NormalY=0 NormalZ=1 AngleXU=0 Radius=1
  constraints (18):
    c: Coincident(g0,g1)
    c: Coincident(g1,g2)
    c: Coincident(g2,g3)
    c: Coincident(g3,g4)
    c: Coincident(g4,g5)
    c: Coincident(g5,g0)
    c: Equal(g0, g1-g5) x5
    c: PointOnObject(g0,g6)
    c: PointOnObject(g1,g6)
    c: PointOnObject(g2,g6)
    c: PointOnObject(g3,g6)
    c: PointOnObject(g4,g6)
    c: PointOnObject(g5,g6)
    c: Coincident(g6,g-1)
    c: PointOnObject(g5,g-2)
    c: DistanceX(g0,g4) = 4
    c: Coincident(g7,g-1)
    c: Radius(g7) = 1
FEATURE [Sketcher::SketchObject] Sketch2269
  MapMode = 5
  Support = -> [XY_Plane898]
FEATURE [Sketcher::SketchObject] Sketch2274
  MapMode = 5
  Support = -> [XY_Plane926]
  sketch-geometry (8):
    g0: LineSegment StartX=0 StartY=2.3094 StartZ=0 EndX=-2 EndY=1.1547 EndZ=0
    g1: LineSegment StartX=-2 StartY=1.1547 StartZ=0 EndX=-2 EndY=-1.1547 EndZ=0
    g2: LineSegment StartX=-2 StartY=-1.1547 StartZ=0 EndX=-2e-16 EndY=-2.3094 EndZ=0
    g3: LineSegment StartX=-2e-16 StartY=-2.3094 StartZ=0 EndX=2 EndY=-1.1547 EndZ=0
    g4: LineSegment StartX=2 StartY=-1.1547 StartZ=0 EndX=2 EndY=1.1547 EndZ=0
    g5: LineSegment StartX=2 StartY=1.1547 StartZ=0 EndX=0 EndY=2.3094 EndZ=0
    g6: Circle [constr] CenterX=0 CenterY=0 CenterZ=0 NormalX=0 NormalY=0 NormalZ=1 AngleXU=0 Radius=2.3094
    g7: Circle CenterX=0 CenterY=0 CenterZ=0 NormalX=0 NormalY=0 NormalZ=1 AngleXU=0 Radius=1
  constraints (18):
    c: Coincident(g0,g1)
    c: Coincident(g1,g2)
    c: Coincident(g2,g3)
    c: Coincident(g3,g4)
    c: Coincident(g4,g5)
    c: Coincident(g5,g0)
    c: Equal(g0, g1-g5) x5
    c: PointOnObject(g0,g6)
    c: PointOnObject(g1,g6)
    c: PointOnObject(g2,g6)
    c: PointOnObject(g3,g6)
    c: PointOnObject(g4,g6)
    c: PointOnObject(g5,g6)
    c: Coincident(g6,g-1)
    c: PointOnObject(g5,g-2)
    c: DistanceX(g0,g4) = 4
    c: Coincident(g7,g-1)
    c: Radius(g7) = 1
FEATURE [Sketcher::SketchObject] Sketch2276
  MapMode = 5
  Support = -> [XY_Plane903]
  sketch-geometry (1):
    g0: Circle CenterX=0 CenterY=0 CenterZ=0 NormalX=0 NormalY=0 NormalZ=1 AngleXU=0 Radius=1.9
  constraints (2):
    c: Coincident(g0,g-1)
    c: Radius(g0) = 1.9
FEATURE [Sketcher::SketchObject] Sketch2280
  MapMode = 5
  Support = -> [XY_Plane932]
  sketch-geometry (8):
    g0: LineSegment StartX=0 StartY=2.3094 StartZ=0 EndX=-2 EndY=1.1547 EndZ=0
    g1: LineSegment StartX=-2 StartY=1.1547 StartZ=0 EndX=-2 EndY=-1.1547 EndZ=0
    g2: LineSegment StartX=-2 StartY=-1.1547 StartZ=0 EndX=-2e-16 EndY=-2.3094 EndZ=0
    g3: LineSegment StartX=-2e-16 StartY=-2.3094 StartZ=0 EndX=2 EndY=-1.1547 EndZ=0
    g4: LineSegment StartX=2 StartY=-1.1547 StartZ=0 EndX=2 EndY=1.1547 EndZ=0
    g5: LineSegment StartX=2 StartY=1.1547 StartZ=0 EndX=0 EndY=2.3094 EndZ=0
    g6: Circle [constr] CenterX=0 CenterY=0 CenterZ=0 NormalX=0 NormalY=0 NormalZ=1 AngleXU=0 Radius=2.3094
    g7: Circle CenterX=0 CenterY=0 CenterZ=0 NormalX=0 NormalY=0 NormalZ=1 AngleXU=0 Radius=1
  constraints (18):
    c: Coincident(g0,g1)
    c: Coincident(g1,g2)
    c: Coincident(g2,g3)
    c: Coincident(g3,g4)
    c: Coincident(g4,g5)
    c: Coincident(g5,g0)
    c: Equal(g0, g1-g5) x5
    c: PointOnObject(g0,g6)
    c: PointOnObject(g1,g6)
    c: PointOnObject(g2,g6)
    c: PointOnObject(g3,g6)
    c: PointOnObject(g4,g6)
    c: PointOnObject(g5,g6)
    c: Coincident(g6,g-1)
    c: PointOnObject(g5,g-2)
    c: DistanceX(g0,g4) = 4
    c: Coincident(g7,g-1)
    c: Radius(g7) = 1
FEATURE [Sketcher::SketchObject] Sketch2281
  MapMode = 5
  Support = -> [XY_Plane901]
FEATURE [Sketcher::SketchObject] Sketch2282
  MapMode = 5
  Support = -> [XY_Plane932]
FEATURE [Sketcher::SketchObject] Sketch2285
  MapMode = 5
  Support = -> [XY_Plane924]
FEATURE [Sketcher::SketchObject] Sketch2286
  MapMode = 5
  Support = -> [XY_Plane924]
FEATURE [Sketcher::SketchObject] Sketch2288
  MapMode = 5
  Support = -> [XY_Plane921]
  sketch-geometry (1):
    g0: Circle CenterX=0 CenterY=0 CenterZ=0 NormalX=0 NormalY=0 NormalZ=1 AngleXU=0 Radius=1.9
  constraints (2):
    c: Coincident(g0,g-1)
    c: Radius(g0) = 1.9
FEATURE [Sketcher::SketchObject] Sketch2290
  MapMode = 5
  Support = -> [XY_Plane909]
  sketch-geometry (8):
    g0: LineSegment StartX=0 StartY=2.3094 StartZ=0 EndX=-2 EndY=1.1547 EndZ=0
    g1: LineSegment StartX=-2 StartY=1.1547 StartZ=0 EndX=-2 EndY=-1.1547 EndZ=0
    g2: LineSegment StartX=-2 StartY=-1.1547 StartZ=0 EndX=-2e-16 EndY=-2.3094 EndZ=0
    g3: LineSegment StartX=-2e-16 StartY=-2.3094 StartZ=0 EndX=2 EndY=-1.1547 EndZ=0
    g4: LineSegment StartX=2 StartY=-1.1547 StartZ=0 EndX=2 EndY=1.1547 EndZ=0
    g5: LineSegment StartX=2 StartY=1.1547 StartZ=0 EndX=0 EndY=2.3094 EndZ=0
    g6: Circle [constr] CenterX=0 CenterY=0 CenterZ=0 NormalX=0 NormalY=0 NormalZ=1 AngleXU=0 Radius=2.3094
    g7: Circle CenterX=0 CenterY=0 CenterZ=0 NormalX=0 NormalY=0 NormalZ=1 AngleXU=0 Radius=1
  constraints (18):
    c: Coincident(g0,g1)
    c: Coincident(g1,g2)
    c: Coincident(g2,g3)
    c: Coincident(g3,g4)
    c: Coincident(g4,g5)
    c: Coincident(g5,g0)
    c: Equal(g0, g1-g5) x5
    c: PointOnObject(g0,g6)
    c: PointOnObject(g1,g6)
    c: PointOnObject(g2,g6)
    c: PointOnObject(g3,g6)
    c: PointOnObject(g4,g6)
    c: PointOnObject(g5,g6)
    c: Coincident(g6,g-1)
    c: PointOnObject(g5,g-2)
    c: DistanceX(g0,g4) = 4
    c: Coincident(g7,g-1)
    c: Radius(g7) = 1
FEATURE [Sketcher::SketchObject] Sketch2291
  MapMode = 5
  Support = -> [XY_Plane924]
  sketch-geometry (8):
    g0: LineSegment StartX=0 StartY=2.3094 StartZ=0 EndX=-2 EndY=1.1547 EndZ=0
    g1: LineSegment StartX=-2 StartY=1.1547 StartZ=0 EndX=-2 EndY=-1.1547 EndZ=0
    g2: LineSegment StartX=-2 StartY=-1.1547 StartZ=0 EndX=-2e-16 EndY=-2.3094 EndZ=0
    g3: LineSegment StartX=-2e-16 StartY=-2.3094 StartZ=0 EndX=2 EndY=-1.1547 EndZ=0
    g4: LineSegment StartX=2 StartY=-1.1547 StartZ=0 EndX=2 EndY=1.1547 EndZ=0
    g5: LineSegment StartX=2 StartY=1.1547 StartZ=0 EndX=0 EndY=2.3094 EndZ=0
    g6: Circle [constr] CenterX=0 CenterY=0 CenterZ=0 NormalX=0 NormalY=0 NormalZ=1 AngleXU=0 Radius=2.3094
    g7: Circle CenterX=0 CenterY=0 CenterZ=0 NormalX=0 NormalY=0 NormalZ=1 AngleXU=0 Radius=1
  constraints (18):
    c: Coincident(g0,g1)
    c: Coincident(g1,g2)
    c: Coincident(g2,g3)
    c: Coincident(g3,g4)
    c: Coincident(g4,g5)
    c: Coincident(g5,g0)
    c: Equal(g0, g1-g5) x5
    c: PointOnObject(g0,g6)
    c: PointOnObject(g1,g6)
    c: PointOnObject(g2,g6)
    c: PointOnObject(g3,g6)
    c: PointOnObject(g4,g6)
    c: PointOnObject(g5,g6)
    c: Coincident(g6,g-1)
    c: PointOnObject(g5,g-2)
    c: DistanceX(g0,g4) = 4
    c: Coincident(g7,g-1)
    c: Radius(g7) = 1
FEATURE [Sketcher::SketchObject] Sketch2292
  MapMode = 5
  Support = -> [XY_Plane909]
FEATURE [Sketcher::SketchObject] Sketch2293
  MapMode = 5
  Support = -> [XY_Plane907]
  sketch-geometry (1):
    g0: Circle CenterX=0 CenterY=0 CenterZ=0 NormalX=0 NormalY=0 NormalZ=1 AngleXU=0 Radius=1.9
  constraints (2):
    c: Coincident(g0,g-1)
    c: Radius(g0) = 1.9
FEATURE [Sketcher::SketchObject] Sketch2294
  MapMode = 5
  Support = -> [XY_Plane925]
  sketch-geometry (1):
    g0: Circle CenterX=0 CenterY=0 CenterZ=0 NormalX=0 NormalY=0 NormalZ=1 AngleXU=0 Radius=1.9
  constraints (2):
    c: Coincident(g0,g-1)
    c: Radius(g0) = 1.9
FEATURE [Sketcher::SketchObject] Sketch2295
  MapMode = 5
  Support = -> [XY_Plane920]
  sketch-geometry (8):
    g0: LineSegment StartX=0 StartY=2.3094 StartZ=0 EndX=-2 EndY=1.1547 EndZ=0
    g1: LineSegment StartX=-2 StartY=1.1547 StartZ=0 EndX=-2 EndY=-1.1547 EndZ=0
    g2: LineSegment StartX=-2 StartY=-1.1547 StartZ=0 EndX=-2e-16 EndY=-2.3094 EndZ=0
    g3: LineSegment StartX=-2e-16 StartY=-2.3094 StartZ=0 EndX=2 EndY=-1.1547 EndZ=0
    g4: LineSegment StartX=2 StartY=-1.1547 StartZ=0 EndX=2 EndY=1.1547 EndZ=0
    g5: LineSegment StartX=2 StartY=1.1547 StartZ=0 EndX=0 EndY=2.3094 EndZ=0
    g6: Circle [constr] CenterX=0 CenterY=0 CenterZ=0 NormalX=0 NormalY=0 NormalZ=1 AngleXU=0 Radius=2.3094
    g7: Circle CenterX=0 CenterY=0 CenterZ=0 NormalX=0 NormalY=0 NormalZ=1 AngleXU=0 Radius=1
  constraints (18):
    c: Coincident(g0,g1)
    c: Coincident(g1,g2)
    c: Coincident(g2,g3)
    c: Coincident(g3,g4)
    c: Coincident(g4,g5)
    c: Coincident(g5,g0)
    c: Equal(g0, g1-g5) x5
    c: PointOnObject(g0,g6)
    c: PointOnObject(g1,g6)
    c: PointOnObject(g2,g6)
    c: PointOnObject(g3,g6)
    c: PointOnObject(g4,g6)
    c: PointOnObject(g5,g6)
    c: Coincident(g6,g-1)
    c: PointOnObject(g5,g-2)
    c: DistanceX(g0,g4) = 4
    c: Coincident(g7,g-1)
    c: Radius(g7) = 1
FEATURE [Sketcher::SketchObject] Sketch2296
  MapMode = 5
  Support = -> [XY_Plane908]
FEATURE [Sketcher::SketchObject] Sketch2298
  MapMode = 5
  Support = -> [XY_Plane919]
  sketch-geometry (1):
    g0: Circle CenterX=0 CenterY=0 CenterZ=0 NormalX=0 NormalY=0 NormalZ=1 AngleXU=0 Radius=1.9
  constraints (2):
    c: Coincident(g0,g-1)
    c: Radius(g0) = 1.9
FEATURE [Sketcher::SketchObject] Sketch2300
  MapMode = 5
  Support = -> [XY_Plane908]
FEATURE [Sketcher::SketchObject] Sketch2301
  MapMode = 5
  Support = -> [XY_Plane918]
  sketch-geometry (8):
    g0: LineSegment StartX=0 StartY=2.3094 StartZ=0 EndX=-2 EndY=1.1547 EndZ=0
    g1: LineSegment StartX=-2 StartY=1.1547 StartZ=0 EndX=-2 EndY=-1.1547 EndZ=0
    g2: LineSegment StartX=-2 StartY=-1.1547 StartZ=0 EndX=-2e-16 EndY=-2.3094 EndZ=0
    g3: LineSegment StartX=-2e-16 StartY=-2.3094 StartZ=0 EndX=2 EndY=-1.1547 EndZ=0
    g4: LineSegment StartX=2 StartY=-1.1547 StartZ=0 EndX=2 EndY=1.1547 EndZ=0
    g5: LineSegment StartX=2 StartY=1.1547 StartZ=0 EndX=0 EndY=2.3094 EndZ=0
    g6: Circle [constr] CenterX=0 CenterY=0 CenterZ=0 NormalX=0 NormalY=0 NormalZ=1 AngleXU=0 Radius=2.3094
    g7: Circle CenterX=0 CenterY=0 CenterZ=0 NormalX=0 NormalY=0 NormalZ=1 AngleXU=0 Radius=1
  constraints (18):
    c: Coincident(g0,g1)
    c: Coincident(g1,g2)
    c: Coincident(g2,g3)
    c: Coincident(g3,g4)
    c: Coincident(g4,g5)
    c: Coincident(g5,g0)
    c: Equal(g0, g1-g5) x5
    c: PointOnObject(g0,g6)
    c: PointOnObject(g1,g6)
    c: PointOnObject(g2,g6)
    c: PointOnObject(g3,g6)
    c: PointOnObject(g4,g6)
    c: PointOnObject(g5,g6)
    c: Coincident(g6,g-1)
    c: PointOnObject(g5,g-2)
    c: DistanceX(g0,g4) = 4
    c: Coincident(g7,g-1)
    c: Radius(g7) = 1
FEATURE [Sketcher::SketchObject] Sketch2302
  MapMode = 5
  Support = -> [XY_Plane909]
FEATURE [Sketcher::SketchObject] Sketch2307
  MapMode = 5
  Support = -> [XY_Plane916]
  sketch-geometry (1):
    g0: Circle CenterX=0 CenterY=0 CenterZ=0 NormalX=0 NormalY=0 NormalZ=1 AngleXU=0 Radius=1.9
  constraints (2):
    c: Coincident(g0,g-1)
    c: Radius(g0) = 1.9
FEATURE [Sketcher::SketchObject] Sketch2311
  MapMode = 5
  Support = -> [XY_Plane908]
  sketch-geometry (8):
    g0: LineSegment StartX=0 StartY=2.3094 StartZ=0 EndX=-2 EndY=1.1547 EndZ=0
    g1: LineSegment StartX=-2 StartY=1.1547 StartZ=0 EndX=-2 EndY=-1.1547 EndZ=0
    g2: LineSegment StartX=-2 StartY=-1.1547 StartZ=0 EndX=-2e-16 EndY=-2.3094 EndZ=0
    g3: LineSegment StartX=-2e-16 StartY=-2.3094 StartZ=0 EndX=2 EndY=-1.1547 EndZ=0
    g4: LineSegment StartX=2 StartY=-1.1547 StartZ=0 EndX=2 EndY=1.1547 EndZ=0
    g5: LineSegment StartX=2 StartY=1.1547 StartZ=0 EndX=0 EndY=2.3094 EndZ=0
    g6: Circle [constr] CenterX=0 CenterY=0 CenterZ=0 NormalX=0 NormalY=0 NormalZ=1 AngleXU=0 Radius=2.3094
    g7: Circle CenterX=0 CenterY=0 CenterZ=0 NormalX=0 NormalY=0 NormalZ=1 AngleXU=0 Radius=1
  constraints (18):
    c: Coincident(g0,g1)
    c: Coincident(g1,g2)
    c: Coincident(g2,g3)
    c: Coincident(g3,g4)
    c: Coincident(g4,g5)
    c: Coincident(g5,g0)
    c: Equal(g0, g1-g5) x5
    c: PointOnObject(g0,g6)
    c: PointOnObject(g1,g6)
    c: PointOnObject(g2,g6)
    c: PointOnObject(g3,g6)
    c: PointOnObject(g4,g6)
    c: PointOnObject(g5,g6)
    c: Coincident(g6,g-1)
    c: PointOnObject(g5,g-2)
    c: DistanceX(g0,g4) = 4
    c: Coincident(g7,g-1)
    c: Radius(g7) = 1
FEATURE [Sketcher::SketchObject] Sketch2313
  MapMode = 5
  Support = -> [XY_Plane920]
FEATURE [Sketcher::SketchObject] Sketch2314
  MapMode = 5
  Support = -> [XY_Plane906]
  sketch-geometry (8):
    g0: LineSegment StartX=0 StartY=2.3094 StartZ=0 EndX=-2 EndY=1.1547 EndZ=0
    g1: LineSegment StartX=-2 StartY=1.1547 StartZ=0 EndX=-2 EndY=-1.1547 EndZ=0
    g2: LineSegment StartX=-2 StartY=-1.1547 StartZ=0 EndX=-2e-16 EndY=-2.3094 EndZ=0
    g3: LineSegment StartX=-2e-16 StartY=-2.3094 StartZ=0 EndX=2 EndY=-1.1547 EndZ=0
    g4: LineSegment StartX=2 StartY=-1.1547 StartZ=0 EndX=2 EndY=1.1547 EndZ=0
    g5: LineSegment StartX=2 StartY=1.1547 StartZ=0 EndX=0 EndY=2.3094 EndZ=0
    g6: Circle [constr] CenterX=0 CenterY=0 CenterZ=0 NormalX=0 NormalY=0 NormalZ=1 AngleXU=0 Radius=2.3094
    g7: Circle CenterX=0 CenterY=0 CenterZ=0 NormalX=0 NormalY=0 NormalZ=1 AngleXU=0 Radius=1
  constraints (18):
    c: Coincident(g0,g1)
    c: Coincident(g1,g2)
    c: Coincident(g2,g3)
    c: Coincident(g3,g4)
    c: Coincident(g4,g5)
    c: Coincident(g5,g0)
    c: Equal(g0, g1-g5) x5
    c: PointOnObject(g0,g6)
    c: PointOnObject(g1,g6)
    c: PointOnObject(g2,g6)
    c: PointOnObject(g3,g6)
    c: PointOnObject(g4,g6)
    c: PointOnObject(g5,g6)
    c: Coincident(g6,g-1)
    c: PointOnObject(g5,g-2)
    c: DistanceX(g0,g4) = 4
    c: Coincident(g7,g-1)
    c: Radius(g7) = 1
FEATURE [Sketcher::SketchObject] Sketch2316
  MapMode = 5
  Support = -> [XY_Plane918]
FEATURE [Sketcher::SketchObject] Sketch2318
  MapMode = 5
  Support = -> [XY_Plane895]
FEATURE [Sketcher::SketchObject] Sketch2319
  MapMode = 5
  Support = -> [XY_Plane899]
  sketch-geometry (1):
    g0: Circle CenterX=0 CenterY=0 CenterZ=0 NormalX=0 NormalY=0 NormalZ=1 AngleXU=0 Radius=1.9
  constraints (2):
    c: Coincident(g0,g-1)
    c: Radius(g0) = 1.9
FEATURE [Sketcher::SketchObject] Sketch2320
  MapMode = 5
  Support = -> [XY_Plane906]
FEATURE [Sketcher::SketchObject] Sketch2324
  MapMode = 5
  Support = -> [XY_Plane906]
FEATURE [Sketcher::SketchObject] Sketch2325
  MapMode = 5
  Support = -> [XY_Plane918]
FEATURE [Sketcher::SketchObject] Sketch2326
  MapMode = 5
  Support = -> [XY_Plane895]
FEATURE [Sketcher::SketchObject] Sketch2328
  MapMode = 5
  Support = -> [XY_Plane922]
  sketch-geometry (1):
    g0: Circle CenterX=0 CenterY=0 CenterZ=0 NormalX=0 NormalY=0 NormalZ=1 AngleXU=0 Radius=1.9
  constraints (2):
    c: Coincident(g0,g-1)
    c: Radius(g0) = 1.9
FEATURE [Sketcher::SketchObject] Sketch2329
  MapMode = 5
  Support = -> [XY_Plane920]
FEATURE [Sketcher::SketchObject] Sketch2331
  MapMode = 5
  Support = -> [XY_Plane933]
FEATURE [Sketcher::SketchObject] Sketch2332
  MapMode = 5
  Support = -> [XY_Plane897]
  sketch-geometry (1):
    g0: Circle CenterX=0 CenterY=0 CenterZ=0 NormalX=0 NormalY=0 NormalZ=1 AngleXU=0 Radius=1.9
  constraints (2):
    c: Coincident(g0,g-1)
    c: Radius(g0) = 1.9
FEATURE [Sketcher::SketchObject] Sketch2333
  MapMode = 5
  Support = -> [XY_Plane898]
  sketch-geometry (8):
    g0: LineSegment StartX=0 StartY=2.3094 StartZ=0 EndX=-2 EndY=1.1547 EndZ=0
    g1: LineSegment StartX=-2 StartY=1.1547 StartZ=0 EndX=-2 EndY=-1.1547 EndZ=0
    g2: LineSegment StartX=-2 StartY=-1.1547 StartZ=0 EndX=-2e-16 EndY=-2.3094 EndZ=0
    g3: LineSegment StartX=-2e-16 StartY=-2.3094 StartZ=0 EndX=2 EndY=-1.1547 EndZ=0
    g4: LineSegment StartX=2 StartY=-1.1547 StartZ=0 EndX=2 EndY=1.1547 EndZ=0
    g5: LineSegment StartX=2 StartY=1.1547 StartZ=0 EndX=0 EndY=2.3094 EndZ=0
    g6: Circle [constr] CenterX=0 CenterY=0 CenterZ=0 NormalX=0 NormalY=0 NormalZ=1 AngleXU=0 Radius=2.3094
    g7: Circle CenterX=0 CenterY=0 CenterZ=0 NormalX=0 NormalY=0 NormalZ=1 AngleXU=0 Radius=1
  constraints (18):
    c: Coincident(g0,g1)
    c: Coincident(g1,g2)
    c: Coincident(g2,g3)
    c: Coincident(g3,g4)
    c: Coincident(g4,g5)
    c: Coincident(g5,g0)
    c: Equal(g0, g1-g5) x5
    c: PointOnObject(g0,g6)
    c: PointOnObject(g1,g6)
    c: PointOnObject(g2,g6)
    c: PointOnObject(g3,g6)
    c: PointOnObject(g4,g6)
    c: PointOnObject(g5,g6)
    c: Coincident(g6,g-1)
    c: PointOnObject(g5,g-2)
    c: DistanceX(g0,g4) = 4
    c: Coincident(g7,g-1)
    c: Radius(g7) = 1
FEATURE [Sketcher::SketchObject] Sketch2334
  MapMode = 5
  Support = -> [XY_Plane926]
FEATURE [Sketcher::SketchObject] Sketch2335
  MapMode = 5
  Support = -> [XY_Plane895]
  sketch-geometry (8):
    g0: LineSegment StartX=0 StartY=2.3094 StartZ=0 EndX=-2 EndY=1.1547 EndZ=0
    g1: LineSegment StartX=-2 StartY=1.1547 StartZ=0 EndX=-2 EndY=-1.1547 EndZ=0
    g2: LineSegment StartX=-2 StartY=-1.1547 StartZ=0 EndX=-2e-16 EndY=-2.3094 EndZ=0
    g3: LineSegment StartX=-2e-16 StartY=-2.3094 StartZ=0 EndX=2 EndY=-1.1547 EndZ=0
    g4: LineSegment StartX=2 StartY=-1.1547 StartZ=0 EndX=2 EndY=1.1547 EndZ=0
    g5: LineSegment StartX=2 StartY=1.1547 StartZ=0 EndX=0 EndY=2.3094 EndZ=0
    g6: Circle [constr] CenterX=0 CenterY=0 CenterZ=0 NormalX=0 NormalY=0 NormalZ=1 AngleXU=0 Radius=2.3094
    g7: Circle CenterX=0 CenterY=0 CenterZ=0 NormalX=0 NormalY=0 NormalZ=1 AngleXU=0 Radius=1
  constraints (18):
    c: Coincident(g0,g1)
    c: Coincident(g1,g2)
    c: Coincident(g2,g3)
    c: Coincident(g3,g4)
    c: Coincident(g4,g5)
    c: Coincident(g5,g0)
    c: Equal(g0, g1-g5) x5
    c: PointOnObject(g0,g6)
    c: PointOnObject(g1,g6)
    c: PointOnObject(g2,g6)
    c: PointOnObject(g3,g6)
    c: PointOnObject(g4,g6)
    c: PointOnObject(g5,g6)
    c: Coincident(g6,g-1)
    c: PointOnObject(g5,g-2)
    c: DistanceX(g0,g4) = 4
    c: Coincident(g7,g-1)
    c: Radius(g7) = 1
FEATURE [Sketcher::SketchObject] Sketch2337
  MapMode = 5
  Support = -> [XY_Plane902]
  sketch-geometry (1):
    g0: Circle CenterX=0 CenterY=0 CenterZ=0 NormalX=0 NormalY=0 NormalZ=1 AngleXU=0 Radius=1.9
  constraints (2):
    c: Coincident(g0,g-1)
    c: Radius(g0) = 1.9
FEATURE [Sketcher::SketchObject] Sketch2338
  MapMode = 5
  Support = -> [XY_Plane929]
  sketch-geometry (1):
    g0: Circle CenterX=0 CenterY=0 CenterZ=0 NormalX=0 NormalY=0 NormalZ=1 AngleXU=0 Radius=1.9
  constraints (2):
    c: Coincident(g0,g-1)
    c: Radius(g0) = 1.9
FEATURE [Sketcher::SketchObject] Sketch2340
  MapMode = 5
  Support = -> [XY_Plane933]
  sketch-geometry (8):
    g0: LineSegment StartX=0 StartY=2.3094 StartZ=0 EndX=-2 EndY=1.1547 EndZ=0
    g1: LineSegment StartX=-2 StartY=1.1547 StartZ=0 EndX=-2 EndY=-1.1547 EndZ=0
    g2: LineSegment StartX=-2 StartY=-1.1547 StartZ=0 EndX=-2e-16 EndY=-2.3094 EndZ=0
    g3: LineSegment StartX=-2e-16 StartY=-2.3094 StartZ=0 EndX=2 EndY=-1.1547 EndZ=0
    g4: LineSegment StartX=2 StartY=-1.1547 StartZ=0 EndX=2 EndY=1.1547 EndZ=0
    g5: LineSegment StartX=2 StartY=1.1547 StartZ=0 EndX=0 EndY=2.3094 EndZ=0
    g6: Circle [constr] CenterX=0 CenterY=0 CenterZ=0 NormalX=0 NormalY=0 NormalZ=1 AngleXU=0 Radius=2.3094
    g7: Circle CenterX=0 CenterY=0 CenterZ=0 NormalX=0 NormalY=0 NormalZ=1 AngleXU=0 Radius=1
  constraints (18):
    c: Coincident(g0,g1)
    c: Coincident(g1,g2)
    c: Coincident(g2,g3)
    c: Coincident(g3,g4)
    c: Coincident(g4,g5)
    c: Coincident(g5,g0)
    c: Equal(g0, g1-g5) x5
    c: PointOnObject(g0,g6)
    c: PointOnObject(g1,g6)
    c: PointOnObject(g2,g6)
    c: PointOnObject(g3,g6)
    c: PointOnObject(g4,g6)
    c: PointOnObject(g5,g6)
    c: Coincident(g6,g-1)
    c: PointOnObject(g5,g-2)
    c: DistanceX(g0,g4) = 4
    c: Coincident(g7,g-1)
    c: Radius(g7) = 1
FEATURE [PartDesign::Pad] Pad990  label="M3x8 Head141"
  Length = 2
  Length2 = 100
  Profile = -> Sketch2288
  Type = 0
FEATURE [Sketcher::SketchObject] Sketch2284
  MapMode = 5
  Placement = pos=(0,0,2) rot=(0,0,1;0rad)
  Support = -> [Pad990]
  sketch-geometry (1):
    g0: Circle CenterX=0 CenterY=0 CenterZ=0 NormalX=0 NormalY=0 NormalZ=1 AngleXU=0 Radius=1
  constraints (2):
    c: Coincident(g0,g-1)
    c: Radius(g0) = 1
FEATURE [PartDesign::Pad] Pad992  label="M3x8 Head142"
  Length = 2
  Length2 = 100
  Profile = -> Sketch2328
  Type = 0
FEATURE [Sketcher::SketchObject] Sketch2327
  MapMode = 5
  Placement = pos=(0,0,2) rot=(0,0,1;0rad)
  Support = -> [Pad992]
  sketch-geometry (1):
    g0: Circle CenterX=0 CenterY=0 CenterZ=0 NormalX=0 NormalY=0 NormalZ=1 AngleXU=0 Radius=1
  constraints (2):
    c: Coincident(g0,g-1)
    c: Radius(g0) = 1
FEATURE [PartDesign::Pad] Pad991  label="M3x8 Thread141"
  BaseFeature = -> Pad992
  Length = 8
  Length2 = 100
  Profile = -> Sketch2327
  Type = 0
FEATURE [Sketcher::SketchObject] Sketch2305
  MapMode = 5
  Placement = pos=(0,0,0) rot=(1,0,0;3.14159rad)
  Support = -> [Pad991]
  sketch-geometry (7):
    g0: LineSegment StartX=0.77 StartY=0.44456 StartZ=0 EndX=0 EndY=0.889119 EndZ=0
    g1: LineSegment StartX=0 StartY=0.889119 StartZ=0 EndX=-0.77 EndY=0.44456 EndZ=0
    g2: LineSegment StartX=-0.77 StartY=0.44456 StartZ=0 EndX=-0.77 EndY=-0.44456 EndZ=0
    g3: LineSegment StartX=-0.77 StartY=-0.44456 StartZ=0 EndX=3.85628e-11 EndY=-0.889119 EndZ=0
    g4: LineSegment StartX=3.85628e-11 StartY=-0.889119 StartZ=0 EndX=0.77 EndY=-0.44456 EndZ=0
    g5: LineSegment StartX=0.77 StartY=-0.44456 StartZ=0 EndX=0.77 EndY=0.44456 EndZ=0
    g6: Circle [constr] CenterX=0 CenterY=0 CenterZ=0 NormalX=0 NormalY=0 NormalZ=1 AngleXU=0 Radius=0.889119
  constraints (16):
    c: Coincident(g0,g1)
    c: Coincident(g1,g2)
    c: Coincident(g2,g3)
    c: Coincident(g3,g4)
    c: Coincident(g4,g5)
    c: Coincident(g5,g0)
    c: Equal(g0, g1-g5) x5
    c: PointOnObject(g0,g6)
    c: PointOnObject(g1,g6)
    c: PointOnObject(g2,g6)
    c: PointOnObject(g3,g6)
    c: PointOnObject(g4,g6)
    c: PointOnObject(g5,g6)
    c: Coincident(g6,g-1)
    c: PointOnObject(g0,g-2)
    c: DistanceX(g1,g0) = 1.54
FEATURE [PartDesign::Pad] Pad994  label="M3x8 Head143"
  Length = 2
  Length2 = 100
  Profile = -> Sketch2294
  Type = 0
FEATURE [Sketcher::SketchObject] Sketch2303
  MapMode = 5
  Placement = pos=(0,0,2) rot=(0,0,1;0rad)
  Support = -> [Pad994]
  sketch-geometry (1):
    g0: Circle CenterX=0 CenterY=0 CenterZ=0 NormalX=0 NormalY=0 NormalZ=1 AngleXU=0 Radius=1
  constraints (2):
    c: Coincident(g0,g-1)
    c: Radius(g0) = 1
FEATURE [PartDesign::Pad] Pad995  label="M3 Nut Primitive191"
  Length = 0.6
  Length2 = 0.6
  Profile = -> Sketch2311
  Type = 4
FEATURE [Sketcher::SketchObject] Sketch2297
  ExternalGeometry = -> [Pad995]
  MapMode = 5
  Placement = pos=(0,0,0) rot=(0.57735,0.57735,0.57735;2.0944rad)
  Support = -> [YZ_Plane912]
  sketch-geometry (6):
    g0: LineSegment StartX=-1.9594 StartY=0.6 StartZ=0 EndX=-2.8094 EndY=0.6 EndZ=0
    g1: LineSegment StartX=-2.8094 StartY=0.6 StartZ=0 EndX=-2.8094 EndY=-0.6 EndZ=0
    g2: LineSegment StartX=-2.8094 StartY=-0.6 StartZ=0 EndX=-1.9594 EndY=-0.6 EndZ=0
    g3: LineSegment StartX=-1.9594 StartY=-0.6 StartZ=0 EndX=-2.3094 EndY=-0.4 EndZ=0
    g4: LineSegment StartX=-2.3094 StartY=-0.4 StartZ=0 EndX=-2.3094 EndY=0.4 EndZ=0
    g5: LineSegment StartX=-2.3094 StartY=0.4 StartZ=0 EndX=-1.9594 EndY=0.6 EndZ=0
  constraints (15):
    c: Horizontal(g0)
    c: Coincident(g0,g1)
    c: Coincident(g1,g2)
    c: Coincident(g2,g3)
    c: Coincident(g3,g4)
    c: Coincident(g4,g5)
    c: Coincident(g5,g0)
    c: Symmetric(g4,g3,g-1)
    c: Symmetric(g0,g2,g-1)
    c: Symmetric(g1,g0,g-1)
    c: DistanceX(g0,g4) = 0.5
    c: DistanceY(g3,g4) = 0.8
    c: DistanceY(g1,g0) = 1.2
    c: PointOnObject(g3,g-3)
    c: DistanceX(g4,g0) = 0.35
FEATURE [PartDesign::Pad] Pad996  label="M3x8 Thread142"
  BaseFeature = -> Pad990
  Length = 8
  Length2 = 100
  Profile = -> Sketch2284
  Type = 0
FEATURE [Sketcher::SketchObject] Sketch2289
  MapMode = 5
  Placement = pos=(0,0,0) rot=(1,0,0;3.14159rad)
  Support = -> [Pad996]
  sketch-geometry (7):
    g0: LineSegment StartX=0.77 StartY=0.44456 StartZ=0 EndX=0 EndY=0.889119 EndZ=0
    g1: LineSegment StartX=0 StartY=0.889119 StartZ=0 EndX=-0.77 EndY=0.44456 EndZ=0
    g2: LineSegment StartX=-0.77 StartY=0.44456 StartZ=0 EndX=-0.77 EndY=-0.44456 EndZ=0
    g3: LineSegment StartX=-0.77 StartY=-0.44456 StartZ=0 EndX=3.85628e-11 EndY=-0.889119 EndZ=0
    g4: LineSegment StartX=3.85628e-11 StartY=-0.889119 StartZ=0 EndX=0.77 EndY=-0.44456 EndZ=0
    g5: LineSegment StartX=0.77 StartY=-0.44456 StartZ=0 EndX=0.77 EndY=0.44456 EndZ=0
    g6: Circle [constr] CenterX=0 CenterY=0 CenterZ=0 NormalX=0 NormalY=0 NormalZ=1 AngleXU=0 Radius=0.889119
  constraints (16):
    c: Coincident(g0,g1)
    c: Coincident(g1,g2)
    c: Coincident(g2,g3)
    c: Coincident(g3,g4)
    c: Coincident(g4,g5)
    c: Coincident(g5,g0)
    c: Equal(g0, g1-g5) x5
    c: PointOnObject(g0,g6)
    c: PointOnObject(g1,g6)
    c: PointOnObject(g2,g6)
    c: PointOnObject(g3,g6)
    c: PointOnObject(g4,g6)
    c: PointOnObject(g5,g6)
    c: Coincident(g6,g-1)
    c: PointOnObject(g0,g-2)
    c: DistanceX(g1,g0) = 1.54
FEATURE [PartDesign::Pocket] Pocket801  label="M3x8 Wrench142"
  BaseFeature = -> Pad991
  Length = 1
  Length2 = 100
  Profile = -> Sketch2305
  Type = 0
FEATURE [PartDesign::Chamfer] Chamfer480  label="M3x8 Smooth140"
  Base = -> Pocket801 [Face11,Edge2,Edge24,Edge3]
  BaseFeature = -> Pocket801
  Size = 0.2
FEATURE [PartDesign::Pad] Pad997  label="M3x8 Thread143"
  BaseFeature = -> Pad994
  Length = 8
  Length2 = 100
  Profile = -> Sketch2303
  Type = 0
FEATURE [Sketcher::SketchObject] Sketch2310
  MapMode = 5
  Placement = pos=(0,0,0) rot=(1,0,0;3.14159rad)
  Support = -> [Pad997]
  sketch-geometry (7):
    g0: LineSegment StartX=0.77 StartY=0.44456 StartZ=0 EndX=0 EndY=0.889119 EndZ=0
    g1: LineSegment StartX=0 StartY=0.889119 StartZ=0 EndX=-0.77 EndY=0.44456 EndZ=0
    g2: LineSegment StartX=-0.77 StartY=0.44456 StartZ=0 EndX=-0.77 EndY=-0.44456 EndZ=0
    g3: LineSegment StartX=-0.77 StartY=-0.44456 StartZ=0 EndX=3.85628e-11 EndY=-0.889119 EndZ=0
    g4: LineSegment StartX=3.85628e-11 StartY=-0.889119 StartZ=0 EndX=0.77 EndY=-0.44456 EndZ=0
    g5: LineSegment StartX=0.77 StartY=-0.44456 StartZ=0 EndX=0.77 EndY=0.44456 EndZ=0
    g6: Circle [constr] CenterX=0 CenterY=0 CenterZ=0 NormalX=0 NormalY=0 NormalZ=1 AngleXU=0 Radius=0.889119
  constraints (16):
    c: Coincident(g0,g1)
    c: Coincident(g1,g2)
    c: Coincident(g2,g3)
    c: Coincident(g3,g4)
    c: Coincident(g4,g5)
    c: Coincident(g5,g0)
    c: Equal(g0, g1-g5) x5
    c: PointOnObject(g0,g6)
    c: PointOnObject(g1,g6)
    c: PointOnObject(g2,g6)
    c: PointOnObject(g3,g6)
    c: PointOnObject(g4,g6)
    c: PointOnObject(g5,g6)
    c: Coincident(g6,g-1)
    c: PointOnObject(g0,g-2)
    c: DistanceX(g1,g0) = 1.54
FEATURE [PartDesign::Groove] Groove203  label="M3 Nut Smooth195"
  Angle = 360
  Axis = (-2e-16,3e-16,1)
  Base = (0,0,0)
  BaseFeature = -> Pad995
  Profile = -> Sketch2297
  ReferenceAxis = -> Sketch2297 [V_Axis]
  Reversed = true
FEATURE [PartDesign::Chamfer] Chamfer476  label="M3 Nut Smooth Hole193"
  Base = -> Groove203 [Edge24,Edge23]
  BaseFeature = -> Groove203
  Size = 0.2
FEATURE [PartDesign::Pad] Pad998  label="M3x8 Head144"
  Length = 2
  Length2 = 100
  Profile = -> Sketch2307
  Type = 0
FEATURE [Sketcher::SketchObject] Sketch2317
  MapMode = 5
  Placement = pos=(0,0,2) rot=(0,0,1;0rad)
  Support = -> [Pad998]
  sketch-geometry (1):
    g0: Circle CenterX=0 CenterY=0 CenterZ=0 NormalX=0 NormalY=0 NormalZ=1 AngleXU=0 Radius=1
  constraints (2):
    c: Coincident(g0,g-1)
    c: Radius(g0) = 1
FEATURE [PartDesign::Pad] Pad999  label="M3x8 Head145"
  Length = 2
  Length2 = 100
  Profile = -> Sketch2298
  Type = 0
FEATURE [Sketcher::SketchObject] Sketch2306
  MapMode = 5
  Placement = pos=(0,0,2) rot=(0,0,1;0rad)
  Support = -> [Pad999]
  sketch-geometry (1):
    g0: Circle CenterX=0 CenterY=0 CenterZ=0 NormalX=0 NormalY=0 NormalZ=1 AngleXU=0 Radius=1
  constraints (2):
    c: Coincident(g0,g-1)
    c: Radius(g0) = 1
FEATURE [PartDesign::Pad] Pad1000  label="M3 Nut Primitive192"
  Length = 0.6
  Length2 = 0.6
  Profile = -> Sketch2290
  Type = 4
FEATURE [Sketcher::SketchObject] Sketch2304
  ExternalGeometry = -> [Pad1000]
  MapMode = 5
  Placement = pos=(0,0,0) rot=(0.57735,0.57735,0.57735;2.0944rad)
  Support = -> [YZ_Plane910]
  sketch-geometry (6):
    g0: LineSegment StartX=-1.9594 StartY=0.6 StartZ=0 EndX=-2.8094 EndY=0.6 EndZ=0
    g1: LineSegment StartX=-2.8094 StartY=0.6 StartZ=0 EndX=-2.8094 EndY=-0.6 EndZ=0
    g2: LineSegment StartX=-2.8094 StartY=-0.6 StartZ=0 EndX=-1.9594 EndY=-0.6 EndZ=0
    g3: LineSegment StartX=-1.9594 StartY=-0.6 StartZ=0 EndX=-2.3094 EndY=-0.4 EndZ=0
    g4: LineSegment StartX=-2.3094 StartY=-0.4 StartZ=0 EndX=-2.3094 EndY=0.4 EndZ=0
    g5: LineSegment StartX=-2.3094 StartY=0.4 StartZ=0 EndX=-1.9594 EndY=0.6 EndZ=0
  constraints (15):
    c: Horizontal(g0)
    c: Coincident(g0,g1)
    c: Coincident(g1,g2)
    c: Coincident(g2,g3)
    c: Coincident(g3,g4)
    c: Coincident(g4,g5)
    c: Coincident(g5,g0)
    c: Symmetric(g4,g3,g-1)
    c: Symmetric(g0,g2,g-1)
    c: Symmetric(g1,g0,g-1)
    c: DistanceX(g0,g4) = 0.5
    c: DistanceY(g3,g4) = 0.8
    c: DistanceY(g1,g0) = 1.2
    c: PointOnObject(g3,g-3)
    c: DistanceX(g4,g0) = 0.35
FEATURE [PartDesign::Groove] Groove200  label="M3 Nut Smooth192"
  Angle = 360
  Axis = (-2e-16,3e-16,1)
  Base = (0,0,0)
  BaseFeature = -> Pad1000
  Profile = -> Sketch2304
  ReferenceAxis = -> Sketch2304 [V_Axis]
  Reversed = true
FEATURE [PartDesign::Chamfer] Chamfer475  label="M3 Nut Smooth Hole192"
  Base = -> Groove200 [Edge24,Edge23]
  BaseFeature = -> Groove200
  Size = 0.2
FEATURE [PartDesign::Pad] Pad1001  label="M3x8 Head146"
  Length = 2
  Length2 = 100
  Profile = -> Sketch2293
  Type = 0
FEATURE [Sketcher::SketchObject] Sketch2308
  MapMode = 5
  Placement = pos=(0,0,2) rot=(0,0,1;0rad)
  Support = -> [Pad1001]
  sketch-geometry (1):
    g0: Circle CenterX=0 CenterY=0 CenterZ=0 NormalX=0 NormalY=0 NormalZ=1 AngleXU=0 Radius=1
  constraints (2):
    c: Coincident(g0,g-1)
    c: Radius(g0) = 1
FEATURE [PartDesign::Pad] Pad1002  label="M3 Nut Primitive193"
  Length = 0.6
  Length2 = 0.6
  Profile = -> Sketch2291
  Type = 4
FEATURE [Sketcher::SketchObject] Sketch2287
  ExternalGeometry = -> [Pad1002]
  MapMode = 5
  Placement = pos=(0,0,0) rot=(0.57735,0.57735,0.57735;2.0944rad)
  Support = -> [YZ_Plane922]
  sketch-geometry (6):
    g0: LineSegment StartX=-1.9594 StartY=0.6 StartZ=0 EndX=-2.8094 EndY=0.6 EndZ=0
    g1: LineSegment StartX=-2.8094 StartY=0.6 StartZ=0 EndX=-2.8094 EndY=-0.6 EndZ=0
    g2: LineSegment StartX=-2.8094 StartY=-0.6 StartZ=0 EndX=-1.9594 EndY=-0.6 EndZ=0
    g3: LineSegment StartX=-1.9594 StartY=-0.6 StartZ=0 EndX=-2.3094 EndY=-0.4 EndZ=0
    g4: LineSegment StartX=-2.3094 StartY=-0.4 StartZ=0 EndX=-2.3094 EndY=0.4 EndZ=0
    g5: LineSegment StartX=-2.3094 StartY=0.4 StartZ=0 EndX=-1.9594 EndY=0.6 EndZ=0
  constraints (15):
    c: Horizontal(g0)
    c: Coincident(g0,g1)
    c: Coincident(g1,g2)
    c: Coincident(g2,g3)
    c: Coincident(g3,g4)
    c: Coincident(g4,g5)
    c: Coincident(g5,g0)
    c: Symmetric(g4,g3,g-1)
    c: Symmetric(g0,g2,g-1)
    c: Symmetric(g1,g0,g-1)
    c: DistanceX(g0,g4) = 0.5
    c: DistanceY(g3,g4) = 0.8
    c: DistanceY(g1,g0) = 1.2
    c: PointOnObject(g3,g-3)
    c: DistanceX(g4,g0) = 0.35
FEATURE [PartDesign::Groove] Groove202  label="M3 Nut Smooth194"
  Angle = 360
  Axis = (-2e-16,3e-16,1)
  Base = (0,0,0)
  BaseFeature = -> Pad1002
  Profile = -> Sketch2287
  ReferenceAxis = -> Sketch2287 [V_Axis]
  Reversed = true
FEATURE [PartDesign::Chamfer] Chamfer482  label="M3 Nut Smooth Hole195"
  Base = -> Groove202 [Edge24,Edge23]
  BaseFeature = -> Groove202
  Size = 0.2
FEATURE [PartDesign::Pocket] Pocket804  label="M3x8 Wrench144"
  BaseFeature = -> Pad996
  Length = 1
  Length2 = 100
  Profile = -> Sketch2289
  Type = 0
FEATURE [PartDesign::Chamfer] Chamfer483  label="M3x8 Smooth142"
  Base = -> Pocket804 [Face11,Edge2,Edge24,Edge3]
  BaseFeature = -> Pocket804
  Size = 0.2
FEATURE [PartDesign::Pocket] Pocket805  label="M3x8 Wrench145"
  BaseFeature = -> Pad997
  Length = 1
  Length2 = 100
  Profile = -> Sketch2310
  Type = 0
FEATURE [PartDesign::Chamfer] Chamfer481  label="M3x8 Smooth141"
  Base = -> Pocket805 [Face11,Edge2,Edge24,Edge3]
  BaseFeature = -> Pocket805
  Size = 0.2
FEATURE [PartDesign::Pad] Pad1003  label="M3x8 Thread144"
  BaseFeature = -> Pad1001
  Length = 8
  Length2 = 100
  Profile = -> Sketch2308
  Type = 0
FEATURE [Sketcher::SketchObject] Sketch2309
  MapMode = 5
  Placement = pos=(0,0,0) rot=(1,0,0;3.14159rad)
  Support = -> [Pad1003]
  sketch-geometry (7):
    g0: LineSegment StartX=0.77 StartY=0.44456 StartZ=0 EndX=0 EndY=0.889119 EndZ=0
    g1: LineSegment StartX=0 StartY=0.889119 StartZ=0 EndX=-0.77 EndY=0.44456 EndZ=0
    g2: LineSegment StartX=-0.77 StartY=0.44456 StartZ=0 EndX=-0.77 EndY=-0.44456 EndZ=0
    g3: LineSegment StartX=-0.77 StartY=-0.44456 StartZ=0 EndX=3.85628e-11 EndY=-0.889119 EndZ=0
    g4: LineSegment StartX=3.85628e-11 StartY=-0.889119 StartZ=0 EndX=0.77 EndY=-0.44456 EndZ=0
    g5: LineSegment StartX=0.77 StartY=-0.44456 StartZ=0 EndX=0.77 EndY=0.44456 EndZ=0
    g6: Circle [constr] CenterX=0 CenterY=0 CenterZ=0 NormalX=0 NormalY=0 NormalZ=1 AngleXU=0 Radius=0.889119
  constraints (16):
    c: Coincident(g0,g1)
    c: Coincident(g1,g2)
    c: Coincident(g2,g3)
    c: Coincident(g3,g4)
    c: Coincident(g4,g5)
    c: Coincident(g5,g0)
    c: Equal(g0, g1-g5) x5
    c: PointOnObject(g0,g6)
    c: PointOnObject(g1,g6)
    c: PointOnObject(g2,g6)
    c: PointOnObject(g3,g6)
    c: PointOnObject(g4,g6)
    c: PointOnObject(g5,g6)
    c: Coincident(g6,g-1)
    c: PointOnObject(g0,g-2)
    c: DistanceX(g1,g0) = 1.54
FEATURE [PartDesign::Pocket] Pocket800  label="M3x8 Wrench141"
  BaseFeature = -> Pad1003
  Length = 1
  Length2 = 100
  Profile = -> Sketch2309
  Type = 0
FEATURE [PartDesign::Chamfer] Chamfer485  label="M3x8 Smooth143"
  Base = -> Pocket800 [Face11,Edge2,Edge24,Edge3]
  BaseFeature = -> Pocket800
  Size = 0.2
FEATURE [PartDesign::Pad] Pad1004  label="M3x8 Thread145"
  BaseFeature = -> Pad999
  Length = 8
  Length2 = 100
  Profile = -> Sketch2306
  Type = 0
FEATURE [Sketcher::SketchObject] Sketch2299
  MapMode = 5
  Placement = pos=(0,0,0) rot=(1,0,0;3.14159rad)
  Support = -> [Pad1004]
  sketch-geometry (7):
    g0: LineSegment StartX=0.77 StartY=0.44456 StartZ=0 EndX=0 EndY=0.889119 EndZ=0
    g1: LineSegment StartX=0 StartY=0.889119 StartZ=0 EndX=-0.77 EndY=0.44456 EndZ=0
    g2: LineSegment StartX=-0.77 StartY=0.44456 StartZ=0 EndX=-0.77 EndY=-0.44456 EndZ=0
    g3: LineSegment StartX=-0.77 StartY=-0.44456 StartZ=0 EndX=3.85628e-11 EndY=-0.889119 EndZ=0
    g4: LineSegment StartX=3.85628e-11 StartY=-0.889119 StartZ=0 EndX=0.77 EndY=-0.44456 EndZ=0
    g5: LineSegment StartX=0.77 StartY=-0.44456 StartZ=0 EndX=0.77 EndY=0.44456 EndZ=0
    g6: Circle [constr] CenterX=0 CenterY=0 CenterZ=0 NormalX=0 NormalY=0 NormalZ=1 AngleXU=0 Radius=0.889119
  constraints (16):
    c: Coincident(g0,g1)
    c: Coincident(g1,g2)
    c: Coincident(g2,g3)
    c: Coincident(g3,g4)
    c: Coincident(g4,g5)
    c: Coincident(g5,g0)
    c: Equal(g0, g1-g5) x5
    c: PointOnObject(g0,g6)
    c: PointOnObject(g1,g6)
    c: PointOnObject(g2,g6)
    c: PointOnObject(g3,g6)
    c: PointOnObject(g4,g6)
    c: PointOnObject(g5,g6)
    c: Coincident(g6,g-1)
    c: PointOnObject(g0,g-2)
    c: DistanceX(g1,g0) = 1.54
FEATURE [PartDesign::Pocket] Pocket803  label="M3x8 Wrench143"
  BaseFeature = -> Pad1004
  Length = 1
  Length2 = 100
  Profile = -> Sketch2299
  Type = 0
FEATURE [PartDesign::Chamfer] Chamfer477  label="M3x8 Smooth138"
  Base = -> Pocket803 [Face11,Edge2,Edge24,Edge3]
  BaseFeature = -> Pocket803
  Size = 0.2
FEATURE [PartDesign::Pad] Pad1005  label="M3 Nut Primitive194"
  Length = 0.6
  Length2 = 0.6
  Profile = -> Sketch2295
  Type = 4
FEATURE [Sketcher::SketchObject] Sketch2315
  ExternalGeometry = -> [Pad1005]
  MapMode = 5
  Placement = pos=(0,0,0) rot=(0.57735,0.57735,0.57735;2.0944rad)
  Support = -> [YZ_Plane920]
  sketch-geometry (6):
    g0: LineSegment StartX=-1.9594 StartY=0.6 StartZ=0 EndX=-2.8094 EndY=0.6 EndZ=0
    g1: LineSegment StartX=-2.8094 StartY=0.6 StartZ=0 EndX=-2.8094 EndY=-0.6 EndZ=0
    g2: LineSegment StartX=-2.8094 StartY=-0.6 StartZ=0 EndX=-1.9594 EndY=-0.6 EndZ=0
    g3: LineSegment StartX=-1.9594 StartY=-0.6 StartZ=0 EndX=-2.3094 EndY=-0.4 EndZ=0
    g4: LineSegment StartX=-2.3094 StartY=-0.4 StartZ=0 EndX=-2.3094 EndY=0.4 EndZ=0
    g5: LineSegment StartX=-2.3094 StartY=0.4 StartZ=0 EndX=-1.9594 EndY=0.6 EndZ=0
  constraints (15):
    c: Horizontal(g0)
    c: Coincident(g0,g1)
    c: Coincident(g1,g2)
    c: Coincident(g2,g3)
    c: Coincident(g3,g4)
    c: Coincident(g4,g5)
    c: Coincident(g5,g0)
    c: Symmetric(g4,g3,g-1)
    c: Symmetric(g0,g2,g-1)
    c: Symmetric(g1,g0,g-1)
    c: DistanceX(g0,g4) = 0.5
    c: DistanceY(g3,g4) = 0.8
    c: DistanceY(g1,g0) = 1.2
    c: PointOnObject(g3,g-3)
    c: DistanceX(g4,g0) = 0.35
FEATURE [PartDesign::Groove] Groove199  label="M3 Nut Smooth191"
  Angle = 360
  Axis = (-2e-16,3e-16,1)
  Base = (0,0,0)
  BaseFeature = -> Pad1005
  Profile = -> Sketch2315
  ReferenceAxis = -> Sketch2315 [V_Axis]
  Reversed = true
FEATURE [PartDesign::Chamfer] Chamfer484  label="M3 Nut Smooth Hole196"
  Base = -> Groove199 [Edge24,Edge23]
  BaseFeature = -> Groove199
  Size = 0.2
FEATURE [PartDesign::Pad] Pad1006  label="M3 Nut Primitive195"
  Length = 0.6
  Length2 = 0.6
  Profile = -> Sketch2301
  Type = 4
FEATURE [Sketcher::SketchObject] Sketch2312
  ExternalGeometry = -> [Pad1006]
  MapMode = 5
  Placement = pos=(0,0,0) rot=(0.57735,0.57735,0.57735;2.0944rad)
  Support = -> [YZ_Plane923]
  sketch-geometry (6):
    g0: LineSegment StartX=-1.9594 StartY=0.6 StartZ=0 EndX=-2.8094 EndY=0.6 EndZ=0
    g1: LineSegment StartX=-2.8094 StartY=0.6 StartZ=0 EndX=-2.8094 EndY=-0.6 EndZ=0
    g2: LineSegment StartX=-2.8094 StartY=-0.6 StartZ=0 EndX=-1.9594 EndY=-0.6 EndZ=0
    g3: LineSegment StartX=-1.9594 StartY=-0.6 StartZ=0 EndX=-2.3094 EndY=-0.4 EndZ=0
    g4: LineSegment StartX=-2.3094 StartY=-0.4 StartZ=0 EndX=-2.3094 EndY=0.4 EndZ=0
    g5: LineSegment StartX=-2.3094 StartY=0.4 StartZ=0 EndX=-1.9594 EndY=0.6 EndZ=0
  constraints (15):
    c: Horizontal(g0)
    c: Coincident(g0,g1)
    c: Coincident(g1,g2)
    c: Coincident(g2,g3)
    c: Coincident(g3,g4)
    c: Coincident(g4,g5)
    c: Coincident(g5,g0)
    c: Symmetric(g4,g3,g-1)
    c: Symmetric(g0,g2,g-1)
    c: Symmetric(g1,g0,g-1)
    c: DistanceX(g0,g4) = 0.5
    c: DistanceY(g3,g4) = 0.8
    c: DistanceY(g1,g0) = 1.2
    c: PointOnObject(g3,g-3)
    c: DistanceX(g4,g0) = 0.35
FEATURE [PartDesign::Groove] Groove201  label="M3 Nut Smooth193"
  Angle = 360
  Axis = (-2e-16,3e-16,1)
  Base = (0,0,0)
  BaseFeature = -> Pad1006
  Profile = -> Sketch2312
  ReferenceAxis = -> Sketch2312 [V_Axis]
  Reversed = true
FEATURE [PartDesign::Chamfer] Chamfer474  label="M3 Nut Smooth Hole191"
  Base = -> Groove201 [Edge24,Edge23]
  BaseFeature = -> Groove201
  Size = 0.2
FEATURE [PartDesign::Pad] Pad1007  label="M3x8 Thread146"
  BaseFeature = -> Pad998
  Length = 8
  Length2 = 100
  Profile = -> Sketch2317
  Type = 0
FEATURE [Sketcher::SketchObject] Sketch2321
  MapMode = 5
  Placement = pos=(0,0,0) rot=(1,0,0;3.14159rad)
  Support = -> [Pad1007]
  sketch-geometry (7):
    g0: LineSegment StartX=0.77 StartY=0.44456 StartZ=0 EndX=0 EndY=0.889119 EndZ=0
    g1: LineSegment StartX=0 StartY=0.889119 StartZ=0 EndX=-0.77 EndY=0.44456 EndZ=0
    g2: LineSegment StartX=-0.77 StartY=0.44456 StartZ=0 EndX=-0.77 EndY=-0.44456 EndZ=0
    g3: LineSegment StartX=-0.77 StartY=-0.44456 StartZ=0 EndX=3.85628e-11 EndY=-0.889119 EndZ=0
    g4: LineSegment StartX=3.85628e-11 StartY=-0.889119 StartZ=0 EndX=0.77 EndY=-0.44456 EndZ=0
    g5: LineSegment StartX=0.77 StartY=-0.44456 StartZ=0 EndX=0.77 EndY=0.44456 EndZ=0
    g6: Circle [constr] CenterX=0 CenterY=0 CenterZ=0 NormalX=0 NormalY=0 NormalZ=1 AngleXU=0 Radius=0.889119
  constraints (16):
    c: Coincident(g0,g1)
    c: Coincident(g1,g2)
    c: Coincident(g2,g3)
    c: Coincident(g3,g4)
    c: Coincident(g4,g5)
    c: Coincident(g5,g0)
    c: Equal(g0, g1-g5) x5
    c: PointOnObject(g0,g6)
    c: PointOnObject(g1,g6)
    c: PointOnObject(g2,g6)
    c: PointOnObject(g3,g6)
    c: PointOnObject(g4,g6)
    c: PointOnObject(g5,g6)
    c: Coincident(g6,g-1)
    c: PointOnObject(g0,g-2)
    c: DistanceX(g1,g0) = 1.54
FEATURE [PartDesign::Pad] Pad1008  label="M3x8 Head147"
  Length = 2
  Length2 = 100
  Profile = -> Sketch2319
  Type = 0
FEATURE [Sketcher::SketchObject] Sketch2322
  MapMode = 5
  Placement = pos=(0,0,2) rot=(0,0,1;0rad)
  Support = -> [Pad1008]
  sketch-geometry (1):
    g0: Circle CenterX=0 CenterY=0 CenterZ=0 NormalX=0 NormalY=0 NormalZ=1 AngleXU=0 Radius=1
  constraints (2):
    c: Coincident(g0,g-1)
    c: Radius(g0) = 1
FEATURE [PartDesign::Pad] Pad1009
  Length = 2
  Length2 = 100
  Profile = -> Sketch2256
  Type = 0
FEATURE [Sketcher::SketchObject] Sketch2259
  MapMode = 5
  Placement = pos=(0,0,2) rot=(0,0,1;0rad)
  Support = -> [Pad1009]
  sketch-geometry (2):
    g0: Circle CenterX=0 CenterY=0 CenterZ=0 NormalX=0 NormalY=0 NormalZ=1 AngleXU=0 Radius=5
    g1: Circle CenterX=0 CenterY=0 CenterZ=0 NormalX=0 NormalY=0 NormalZ=1 AngleXU=0 Radius=3.5
  constraints (4):
    c: Coincident(g0,g-1)
    c: Coincident(g1,g0)
    c: Radius(g1) = 3.5
    c: Radius(g0) = 5
FEATURE [PartDesign::Pad] Pad1010  label="M3x8 Head148"
  Length = 2
  Length2 = 100
  Profile = -> Sketch2332
  Type = 0
FEATURE [Sketcher::SketchObject] Sketch2262
  MapMode = 5
  Placement = pos=(0,0,2) rot=(0,0,1;0rad)
  Support = -> [Pad1010]
  sketch-geometry (1):
    g0: Circle CenterX=0 CenterY=0 CenterZ=0 NormalX=0 NormalY=0 NormalZ=1 AngleXU=0 Radius=1
  constraints (2):
    c: Coincident(g0,g-1)
    c: Radius(g0) = 1
FEATURE [PartDesign::Pocket] Pocket806  label="M3x8 Wrench146"
  BaseFeature = -> Pad1007
  Length = 1
  Length2 = 100
  Profile = -> Sketch2321
  Type = 0
FEATURE [PartDesign::Chamfer] Chamfer479  label="M3x8 Smooth139"
  Base = -> Pocket806 [Face11,Edge2,Edge24,Edge3]
  BaseFeature = -> Pocket806
  Size = 0.2
FEATURE [PartDesign::Pad] Pad1011  label="M3 Nut Primitive196"
  Length = 0.6
  Length2 = 0.6
  Profile = -> Sketch2314
  Type = 4
FEATURE [Sketcher::SketchObject] Sketch2323
  ExternalGeometry = -> [Pad1011]
  MapMode = 5
  Placement = pos=(0,0,0) rot=(0.57735,0.57735,0.57735;2.0944rad)
  Support = -> [YZ_Plane914]
  sketch-geometry (6):
    g0: LineSegment StartX=-1.9594 StartY=0.6 StartZ=0 EndX=-2.8094 EndY=0.6 EndZ=0
    g1: LineSegment StartX=-2.8094 StartY=0.6 StartZ=0 EndX=-2.8094 EndY=-0.6 EndZ=0
    g2: LineSegment StartX=-2.8094 StartY=-0.6 StartZ=0 EndX=-1.9594 EndY=-0.6 EndZ=0
    g3: LineSegment StartX=-1.9594 StartY=-0.6 StartZ=0 EndX=-2.3094 EndY=-0.4 EndZ=0
    g4: LineSegment StartX=-2.3094 StartY=-0.4 StartZ=0 EndX=-2.3094 EndY=0.4 EndZ=0
    g5: LineSegment StartX=-2.3094 StartY=0.4 StartZ=0 EndX=-1.9594 EndY=0.6 EndZ=0
  constraints (15):
    c: Horizontal(g0)
    c: Coincident(g0,g1)
    c: Coincident(g1,g2)
    c: Coincident(g2,g3)
    c: Coincident(g3,g4)
    c: Coincident(g4,g5)
    c: Coincident(g5,g0)
    c: Symmetric(g4,g3,g-1)
    c: Symmetric(g0,g2,g-1)
    c: Symmetric(g1,g0,g-1)
    c: DistanceX(g0,g4) = 0.5
    c: DistanceY(g3,g4) = 0.8
    c: DistanceY(g1,g0) = 1.2
    c: PointOnObject(g3,g-3)
    c: DistanceX(g4,g0) = 0.35
FEATURE [PartDesign::Groove] Groove204  label="M3 Nut Smooth196"
  Angle = 360
  Axis = (-2e-16,3e-16,1)
  Base = (0,0,0)
  BaseFeature = -> Pad1011
  Profile = -> Sketch2323
  ReferenceAxis = -> Sketch2323 [V_Axis]
  Reversed = true
FEATURE [PartDesign::Chamfer] Chamfer478  label="M3 Nut Smooth Hole194"
  Base = -> Groove204 [Edge24,Edge23]
  BaseFeature = -> Groove204
  Size = 0.2
FEATURE [PartDesign::Pocket] Pocket807
  BaseFeature = -> Pad1009
  Length = 1
  Length2 = 100
  Profile = -> Sketch2259
  Type = 0
FEATURE [Sketcher::SketchObject] Sketch2254
  MapMode = 5
  Placement = pos=(0,0,2) rot=(0,0,1;0rad)
  Support = -> [Pocket807]
  sketch-geometry (1):
    g0: Circle CenterX=0 CenterY=0 CenterZ=0 NormalX=0 NormalY=0 NormalZ=1 AngleXU=0 Radius=3
  constraints (2):
    c: Coincident(g0,g-1)
    c: Radius(g0) = 3
FEATURE [PartDesign::Pad] Pad1014  label="M3x8 Head149"
  Length = 2
  Length2 = 100
  Profile = -> Sketch2261
  Type = 0
FEATURE [Sketcher::SketchObject] Sketch2258
  MapMode = 5
  Placement = pos=(0,0,2) rot=(0,0,1;0rad)
  Support = -> [Pad1014]
  sketch-geometry (1):
    g0: Circle CenterX=0 CenterY=0 CenterZ=0 NormalX=0 NormalY=0 NormalZ=1 AngleXU=0 Radius=1
  constraints (2):
    c: Coincident(g0,g-1)
    c: Radius(g0) = 1
FEATURE [PartDesign::Pad] Pad1013  label="M3x8 Thread147"
  BaseFeature = -> Pad1014
  Length = 8
  Length2 = 100
  Profile = -> Sketch2258
  Type = 0
FEATURE [Sketcher::SketchObject] Sketch2268
  MapMode = 5
  Placement = pos=(0,0,0) rot=(1,0,0;3.14159rad)
  Support = -> [Pad1013]
  sketch-geometry (7):
    g0: LineSegment StartX=0.77 StartY=0.44456 StartZ=0 EndX=0 EndY=0.889119 EndZ=0
    g1: LineSegment StartX=0 StartY=0.889119 StartZ=0 EndX=-0.77 EndY=0.44456 EndZ=0
    g2: LineSegment StartX=-0.77 StartY=0.44456 StartZ=0 EndX=-0.77 EndY=-0.44456 EndZ=0
    g3: LineSegment StartX=-0.77 StartY=-0.44456 StartZ=0 EndX=3.85628e-11 EndY=-0.889119 EndZ=0
    g4: LineSegment StartX=3.85628e-11 StartY=-0.889119 StartZ=0 EndX=0.77 EndY=-0.44456 EndZ=0
    g5: LineSegment StartX=0.77 StartY=-0.44456 StartZ=0 EndX=0.77 EndY=0.44456 EndZ=0
    g6: Circle [constr] CenterX=0 CenterY=0 CenterZ=0 NormalX=0 NormalY=0 NormalZ=1 AngleXU=0 Radius=0.889119
  constraints (16):
    c: Coincident(g0,g1)
    c: Coincident(g1,g2)
    c: Coincident(g2,g3)
    c: Coincident(g3,g4)
    c: Coincident(g4,g5)
    c: Coincident(g5,g0)
    c: Equal(g0, g1-g5) x5
    c: PointOnObject(g0,g6)
    c: PointOnObject(g1,g6)
    c: PointOnObject(g2,g6)
    c: PointOnObject(g3,g6)
    c: PointOnObject(g4,g6)
    c: PointOnObject(g5,g6)
    c: Coincident(g6,g-1)
    c: PointOnObject(g0,g-2)
    c: DistanceX(g1,g0) = 1.54
FEATURE [PartDesign::Pad] Pad1015  label="M3 Nut Primitive197"
  Length = 0.6
  Length2 = 0.6
  Profile = -> Sketch2266
  Type = 4
FEATURE [Sketcher::SketchObject] Sketch2279
  ExternalGeometry = -> [Pad1015]
  MapMode = 5
  Placement = pos=(0,0,0) rot=(0.57735,0.57735,0.57735;2.0944rad)
  Support = -> [YZ_Plane890]
  sketch-geometry (6):
    g0: LineSegment StartX=-1.9594 StartY=0.6 StartZ=0 EndX=-2.8094 EndY=0.6 EndZ=0
    g1: LineSegment StartX=-2.8094 StartY=0.6 StartZ=0 EndX=-2.8094 EndY=-0.6 EndZ=0
    g2: LineSegment StartX=-2.8094 StartY=-0.6 StartZ=0 EndX=-1.9594 EndY=-0.6 EndZ=0
    g3: LineSegment StartX=-1.9594 StartY=-0.6 StartZ=0 EndX=-2.3094 EndY=-0.4 EndZ=0
    g4: LineSegment StartX=-2.3094 StartY=-0.4 StartZ=0 EndX=-2.3094 EndY=0.4 EndZ=0
    g5: LineSegment StartX=-2.3094 StartY=0.4 StartZ=0 EndX=-1.9594 EndY=0.6 EndZ=0
  constraints (15):
    c: Horizontal(g0)
    c: Coincident(g0,g1)
    c: Coincident(g1,g2)
    c: Coincident(g2,g3)
    c: Coincident(g3,g4)
    c: Coincident(g4,g5)
    c: Coincident(g5,g0)
    c: Symmetric(g4,g3,g-1)
    c: Symmetric(g0,g2,g-1)
    c: Symmetric(g1,g0,g-1)
    c: DistanceX(g0,g4) = 0.5
    c: DistanceY(g3,g4) = 0.8
    c: DistanceY(g1,g0) = 1.2
    c: PointOnObject(g3,g-3)
    c: DistanceX(g4,g0) = 0.35
FEATURE [PartDesign::Groove] Groove207  label="M3 Nut Smooth199"
  Angle = 360
  Axis = (-2e-16,3e-16,1)
  Base = (0,0,0)
  BaseFeature = -> Pad1015
  Profile = -> Sketch2279
  ReferenceAxis = -> Sketch2279 [V_Axis]
  Reversed = true
FEATURE [PartDesign::Chamfer] Chamfer491  label="M3 Nut Smooth Hole199"
  Base = -> Groove207 [Edge24,Edge23]
  BaseFeature = -> Groove207
  Size = 0.2
FEATURE [PartDesign::Pocket] Pocket810  label="M3x8 Wrench148"
  BaseFeature = -> Pad1013
  Length = 1
  Length2 = 100
  Profile = -> Sketch2268
  Type = 0
FEATURE [PartDesign::Chamfer] Chamfer486  label="M3x8 Smooth144"
  Base = -> Pocket810 [Face11,Edge2,Edge24,Edge3]
  BaseFeature = -> Pocket810
  Size = 0.2
FEATURE [PartDesign::Pad] Pad1017  label="M3 Nut Primitive198"
  Length = 0.6
  Length2 = 0.6
  Profile = -> Sketch2280
  Type = 4
FEATURE [Sketcher::SketchObject] Sketch2283
  ExternalGeometry = -> [Pad1017]
  MapMode = 5
  Placement = pos=(0,0,0) rot=(0.57735,0.57735,0.57735;2.0944rad)
  Support = -> [YZ_Plane898]
  sketch-geometry (6):
    g0: LineSegment StartX=-1.9594 StartY=0.6 StartZ=0 EndX=-2.8094 EndY=0.6 EndZ=0
    g1: LineSegment StartX=-2.8094 StartY=0.6 StartZ=0 EndX=-2.8094 EndY=-0.6 EndZ=0
    g2: LineSegment StartX=-2.8094 StartY=-0.6 StartZ=0 EndX=-1.9594 EndY=-0.6 EndZ=0
    g3: LineSegment StartX=-1.9594 StartY=-0.6 StartZ=0 EndX=-2.3094 EndY=-0.4 EndZ=0
    g4: LineSegment StartX=-2.3094 StartY=-0.4 StartZ=0 EndX=-2.3094 EndY=0.4 EndZ=0
    g5: LineSegment StartX=-2.3094 StartY=0.4 StartZ=0 EndX=-1.9594 EndY=0.6 EndZ=0
  constraints (15):
    c: Horizontal(g0)
    c: Coincident(g0,g1)
    c: Coincident(g1,g2)
    c: Coincident(g2,g3)
    c: Coincident(g3,g4)
    c: Coincident(g4,g5)
    c: Coincident(g5,g0)
    c: Symmetric(g4,g3,g-1)
    c: Symmetric(g0,g2,g-1)
    c: Symmetric(g1,g0,g-1)
    c: DistanceX(g0,g4) = 0.5
    c: DistanceY(g3,g4) = 0.8
    c: DistanceY(g1,g0) = 1.2
    c: PointOnObject(g3,g-3)
    c: DistanceX(g4,g0) = 0.35
FEATURE [PartDesign::Groove] Groove208  label="M3 Nut Smooth200"
  Angle = 360
  Axis = (-2e-16,3e-16,1)
  Base = (0,0,0)
  BaseFeature = -> Pad1017
  Profile = -> Sketch2283
  ReferenceAxis = -> Sketch2283 [V_Axis]
  Reversed = true
FEATURE [PartDesign::Chamfer] Chamfer494  label="M3 Nut Smooth Hole201"
  Base = -> Groove208 [Edge24,Edge23]
  BaseFeature = -> Groove208
  Size = 0.2
FEATURE [PartDesign::Pad] Pad1018  label="M3x8 Thread149"
  BaseFeature = -> Pad1008
  Length = 8
  Length2 = 100
  Profile = -> Sketch2322
  Type = 0
FEATURE [Sketcher::SketchObject] Sketch2336
  MapMode = 5
  Placement = pos=(0,0,0) rot=(1,0,0;3.14159rad)
  Support = -> [Pad1018]
  sketch-geometry (7):
    g0: LineSegment StartX=0.77 StartY=0.44456 StartZ=0 EndX=0 EndY=0.889119 EndZ=0
    g1: LineSegment StartX=0 StartY=0.889119 StartZ=0 EndX=-0.77 EndY=0.44456 EndZ=0
    g2: LineSegment StartX=-0.77 StartY=0.44456 StartZ=0 EndX=-0.77 EndY=-0.44456 EndZ=0
    g3: LineSegment StartX=-0.77 StartY=-0.44456 StartZ=0 EndX=3.85628e-11 EndY=-0.889119 EndZ=0
    g4: LineSegment StartX=3.85628e-11 StartY=-0.889119 StartZ=0 EndX=0.77 EndY=-0.44456 EndZ=0
    g5: LineSegment StartX=0.77 StartY=-0.44456 StartZ=0 EndX=0.77 EndY=0.44456 EndZ=0
    g6: Circle [constr] CenterX=0 CenterY=0 CenterZ=0 NormalX=0 NormalY=0 NormalZ=1 AngleXU=0 Radius=0.889119
  constraints (16):
    c: Coincident(g0,g1)
    c: Coincident(g1,g2)
    c: Coincident(g2,g3)
    c: Coincident(g3,g4)
    c: Coincident(g4,g5)
    c: Coincident(g5,g0)
    c: Equal(g0, g1-g5) x5
    c: PointOnObject(g0,g6)
    c: PointOnObject(g1,g6)
    c: PointOnObject(g2,g6)
    c: PointOnObject(g3,g6)
    c: PointOnObject(g4,g6)
    c: PointOnObject(g5,g6)
    c: Coincident(g6,g-1)
    c: PointOnObject(g0,g-2)
    c: DistanceX(g1,g0) = 1.54
FEATURE [PartDesign::Pad] Pad1019  label="M3 Nut Primitive199"
  Length = 0.6
  Length2 = 0.6
  Profile = -> Sketch2274
  Type = 4
FEATURE [Sketcher::SketchObject] Sketch2339
  ExternalGeometry = -> [Pad1019]
  MapMode = 5
  Placement = pos=(0,0,0) rot=(0.57735,0.57735,0.57735;2.0944rad)
  Support = -> [YZ_Plane894]
  sketch-geometry (6):
    g0: LineSegment StartX=-1.9594 StartY=0.6 StartZ=0 EndX=-2.8094 EndY=0.6 EndZ=0
    g1: LineSegment StartX=-2.8094 StartY=0.6 StartZ=0 EndX=-2.8094 EndY=-0.6 EndZ=0
    g2: LineSegment StartX=-2.8094 StartY=-0.6 StartZ=0 EndX=-1.9594 EndY=-0.6 EndZ=0
    g3: LineSegment StartX=-1.9594 StartY=-0.6 StartZ=0 EndX=-2.3094 EndY=-0.4 EndZ=0
    g4: LineSegment StartX=-2.3094 StartY=-0.4 StartZ=0 EndX=-2.3094 EndY=0.4 EndZ=0
    g5: LineSegment StartX=-2.3094 StartY=0.4 StartZ=0 EndX=-1.9594 EndY=0.6 EndZ=0
  constraints (15):
    c: Horizontal(g0)
    c: Coincident(g0,g1)
    c: Coincident(g1,g2)
    c: Coincident(g2,g3)
    c: Coincident(g3,g4)
    c: Coincident(g4,g5)
    c: Coincident(g5,g0)
    c: Symmetric(g4,g3,g-1)
    c: Symmetric(g0,g2,g-1)
    c: Symmetric(g1,g0,g-1)
    c: DistanceX(g0,g4) = 0.5
    c: DistanceY(g3,g4) = 0.8
    c: DistanceY(g1,g0) = 1.2
    c: PointOnObject(g3,g-3)
    c: DistanceX(g4,g0) = 0.35
FEATURE [PartDesign::Groove] Groove209  label="M3 Nut Smooth201"
  Angle = 360
  Axis = (-2e-16,3e-16,1)
  Base = (0,0,0)
  BaseFeature = -> Pad1019
  Profile = -> Sketch2339
  ReferenceAxis = -> Sketch2339 [V_Axis]
  Reversed = true
FEATURE [PartDesign::Chamfer] Chamfer493  label="M3 Nut Smooth Hole200"
  Base = -> Groove209 [Edge24,Edge23]
  BaseFeature = -> Groove209
  Size = 0.2
FEATURE [PartDesign::Pad] Pad1020  label="M3x8 Thread150"
  BaseFeature = -> Pad1010
  Length = 8
  Length2 = 100
  Profile = -> Sketch2262
  Type = 0
FEATURE [Sketcher::SketchObject] Sketch2271
  MapMode = 5
  Placement = pos=(0,0,0) rot=(1,0,0;3.14159rad)
  Support = -> [Pad1020]
  sketch-geometry (7):
    g0: LineSegment StartX=0.77 StartY=0.44456 StartZ=0 EndX=0 EndY=0.889119 EndZ=0
    g1: LineSegment StartX=0 StartY=0.889119 StartZ=0 EndX=-0.77 EndY=0.44456 EndZ=0
    g2: LineSegment StartX=-0.77 StartY=0.44456 StartZ=0 EndX=-0.77 EndY=-0.44456 EndZ=0
    g3: LineSegment StartX=-0.77 StartY=-0.44456 StartZ=0 EndX=3.85628e-11 EndY=-0.889119 EndZ=0
    g4: LineSegment StartX=3.85628e-11 StartY=-0.889119 StartZ=0 EndX=0.77 EndY=-0.44456 EndZ=0
    g5: LineSegment StartX=0.77 StartY=-0.44456 StartZ=0 EndX=0.77 EndY=0.44456 EndZ=0
    g6: Circle [constr] CenterX=0 CenterY=0 CenterZ=0 NormalX=0 NormalY=0 NormalZ=1 AngleXU=0 Radius=0.889119
  constraints (16):
    c: Coincident(g0,g1)
    c: Coincident(g1,g2)
    c: Coincident(g2,g3)
    c: Coincident(g3,g4)
    c: Coincident(g4,g5)
    c: Coincident(g5,g0)
    c: Equal(g0, g1-g5) x5
    c: PointOnObject(g0,g6)
    c: PointOnObject(g1,g6)
    c: PointOnObject(g2,g6)
    c: PointOnObject(g3,g6)
    c: PointOnObject(g4,g6)
    c: PointOnObject(g5,g6)
    c: Coincident(g6,g-1)
    c: PointOnObject(g0,g-2)
    c: DistanceX(g1,g0) = 1.54
FEATURE [PartDesign::Pad] Pad1021  label="M3x8 Head150"
  Length = 2
  Length2 = 100
  Profile = -> Sketch2276
  Type = 0
FEATURE [Sketcher::SketchObject] Sketch2273
  MapMode = 5
  Placement = pos=(0,0,2) rot=(0,0,1;0rad)
  Support = -> [Pad1021]
  sketch-geometry (1):
    g0: Circle CenterX=0 CenterY=0 CenterZ=0 NormalX=0 NormalY=0 NormalZ=1 AngleXU=0 Radius=1
  constraints (2):
    c: Coincident(g0,g-1)
    c: Radius(g0) = 1
FEATURE [PartDesign::Pad] Pad1016  label="M3x8 Thread148"
  BaseFeature = -> Pad1021
  Length = 8
  Length2 = 100
  Profile = -> Sketch2273
  Type = 0
FEATURE [Sketcher::SketchObject] Sketch2272
  MapMode = 5
  Placement = pos=(0,0,0) rot=(1,0,0;3.14159rad)
  Support = -> [Pad1016]
  sketch-geometry (7):
    g0: LineSegment StartX=0.77 StartY=0.44456 StartZ=0 EndX=0 EndY=0.889119 EndZ=0
    g1: LineSegment StartX=0 StartY=0.889119 StartZ=0 EndX=-0.77 EndY=0.44456 EndZ=0
    g2: LineSegment StartX=-0.77 StartY=0.44456 StartZ=0 EndX=-0.77 EndY=-0.44456 EndZ=0
    g3: LineSegment StartX=-0.77 StartY=-0.44456 StartZ=0 EndX=3.85628e-11 EndY=-0.889119 EndZ=0
    g4: LineSegment StartX=3.85628e-11 StartY=-0.889119 StartZ=0 EndX=0.77 EndY=-0.44456 EndZ=0
    g5: LineSegment StartX=0.77 StartY=-0.44456 StartZ=0 EndX=0.77 EndY=0.44456 EndZ=0
    g6: Circle [constr] CenterX=0 CenterY=0 CenterZ=0 NormalX=0 NormalY=0 NormalZ=1 AngleXU=0 Radius=0.889119
  constraints (16):
    c: Coincident(g0,g1)
    c: Coincident(g1,g2)
    c: Coincident(g2,g3)
    c: Coincident(g3,g4)
    c: Coincident(g4,g5)
    c: Coincident(g5,g0)
    c: Equal(g0, g1-g5) x5
    c: PointOnObject(g0,g6)
    c: PointOnObject(g1,g6)
    c: PointOnObject(g2,g6)
    c: PointOnObject(g3,g6)
    c: PointOnObject(g4,g6)
    c: PointOnObject(g5,g6)
    c: Coincident(g6,g-1)
    c: PointOnObject(g0,g-2)
    c: DistanceX(g1,g0) = 1.54
FEATURE [PartDesign::Pocket] Pocket811  label="M3x8 Wrench149"
  BaseFeature = -> Pad1016
  Length = 1
  Length2 = 100
  Profile = -> Sketch2272
  Type = 0
FEATURE [PartDesign::Chamfer] Chamfer488  label="M3x8 Smooth145"
  Base = -> Pocket811 [Face11,Edge2,Edge24,Edge3]
  BaseFeature = -> Pocket811
  Size = 0.2
FEATURE [PartDesign::Pad] Pad1022  label="M3x8 Head151"
  Length = 2
  Length2 = 100
  Profile = -> Sketch2337
  Type = 0
FEATURE [Sketcher::SketchObject] Sketch2275
  MapMode = 5
  Placement = pos=(0,0,2) rot=(0,0,1;0rad)
  Support = -> [Pad1022]
  sketch-geometry (1):
    g0: Circle CenterX=0 CenterY=0 CenterZ=0 NormalX=0 NormalY=0 NormalZ=1 AngleXU=0 Radius=1
  constraints (2):
    c: Coincident(g0,g-1)
    c: Radius(g0) = 1
FEATURE [PartDesign::Pocket] Pocket812
  BaseFeature = -> Pocket807
  Length = 1
  Length2 = 100
  Profile = -> Sketch2254
  Type = 0
FEATURE [Sketcher::SketchObject] Sketch2260
  MapMode = 5
  Placement = pos=(0,0,1) rot=(0,0,1;0rad)
  Support = -> [Pocket812]
  sketch-geometry (1):
    g0: Circle CenterX=0 CenterY=0 CenterZ=0 NormalX=0 NormalY=0 NormalZ=1 AngleXU=0 Radius=1.5
  constraints (2):
    c: Coincident(g0,g-1)
    c: Radius(g0) = 1.5
FEATURE [PartDesign::Pocket] Pocket808
  BaseFeature = -> Pocket812
  Length = 5
  Length2 = 100
  Profile = -> Sketch2260
  Type = 0
FEATURE [Sketcher::SketchObject] Sketch2257
  MapMode = 5
  Placement = pos=(0,0,0) rot=(1,0,0;3.14159rad)
  Support = -> [Pocket808]
  sketch-geometry (2):
    g0: Circle CenterX=0 CenterY=0 CenterZ=0 NormalX=0 NormalY=0 NormalZ=1 AngleXU=0 Radius=4.5
    g1: Circle CenterX=0 CenterY=0 CenterZ=0 NormalX=0 NormalY=0 NormalZ=1 AngleXU=0 Radius=3
  constraints (4):
    c: Coincident(g0,g-1)
    c: Coincident(g1,g0)
    c: Radius(g0) = 4.5
    c: Radius(g1) = 3
FEATURE [PartDesign::Pad] Pad1012
  BaseFeature = -> Pocket808
  Length = 3
  Length2 = 100
  Profile = -> Sketch2257
  Type = 0
FEATURE [PartDesign::Fillet] Fillet253
  Base = -> Pad1012 [Face5,Edge96,Face4]
  BaseFeature = -> Pad1012
  Radius = 0.2
FEATURE [PartDesign::Pad] Pad1023  label="M3 Nut Primitive200"
  Length = 0.6
  Length2 = 0.6
  Profile = -> Sketch2340
  Type = 4
FEATURE [Sketcher::SketchObject] Sketch2267
  ExternalGeometry = -> [Pad1023]
  MapMode = 5
  Placement = pos=(0,0,0) rot=(0.57735,0.57735,0.57735;2.0944rad)
  Support = -> [YZ_Plane899]
  sketch-geometry (6):
    g0: LineSegment StartX=-1.9594 StartY=0.6 StartZ=0 EndX=-2.8094 EndY=0.6 EndZ=0
    g1: LineSegment StartX=-2.8094 StartY=0.6 StartZ=0 EndX=-2.8094 EndY=-0.6 EndZ=0
    g2: LineSegment StartX=-2.8094 StartY=-0.6 StartZ=0 EndX=-1.9594 EndY=-0.6 EndZ=0
    g3: LineSegment StartX=-1.9594 StartY=-0.6 StartZ=0 EndX=-2.3094 EndY=-0.4 EndZ=0
    g4: LineSegment StartX=-2.3094 StartY=-0.4 StartZ=0 EndX=-2.3094 EndY=0.4 EndZ=0
    g5: LineSegment StartX=-2.3094 StartY=0.4 StartZ=0 EndX=-1.9594 EndY=0.6 EndZ=0
  constraints (15):
    c: Horizontal(g0)
    c: Coincident(g0,g1)
    c: Coincident(g1,g2)
    c: Coincident(g2,g3)
    c: Coincident(g3,g4)
    c: Coincident(g4,g5)
    c: Coincident(g5,g0)
    c: Symmetric(g4,g3,g-1)
    c: Symmetric(g0,g2,g-1)
    c: Symmetric(g1,g0,g-1)
    c: DistanceX(g0,g4) = 0.5
    c: DistanceY(g3,g4) = 0.8
    c: DistanceY(g1,g0) = 1.2
    c: PointOnObject(g3,g-3)
    c: DistanceX(g4,g0) = 0.35
FEATURE [PartDesign::Groove] Groove206  label="M3 Nut Smooth198"
  Angle = 360
  Axis = (-2e-16,3e-16,1)
  Base = (0,0,0)
  BaseFeature = -> Pad1023
  Profile = -> Sketch2267
  ReferenceAxis = -> Sketch2267 [V_Axis]
  Reversed = true
FEATURE [PartDesign::Chamfer] Chamfer490  label="M3 Nut Smooth Hole198"
  Base = -> Groove206 [Edge24,Edge23]
  BaseFeature = -> Groove206
  Size = 0.2
FEATURE [PartDesign::Pad] Pad1024  label="M3x8 Head152"
  Length = 2
  Length2 = 100
  Profile = -> Sketch2338
  Type = 0
FEATURE [Sketcher::SketchObject] Sketch2277
  MapMode = 5
  Placement = pos=(0,0,2) rot=(0,0,1;0rad)
  Support = -> [Pad1024]
  sketch-geometry (1):
    g0: Circle CenterX=0 CenterY=0 CenterZ=0 NormalX=0 NormalY=0 NormalZ=1 AngleXU=0 Radius=1
  constraints (2):
    c: Coincident(g0,g-1)
    c: Radius(g0) = 1
FEATURE [PartDesign::Pad] Pad1025  label="M3 Nut Primitive201"
  Length = 0.6
  Length2 = 0.6
  Profile = -> Sketch2335
  Type = 4
FEATURE [Sketcher::SketchObject] Sketch2330
  ExternalGeometry = -> [Pad1025]
  MapMode = 5
  Placement = pos=(0,0,0) rot=(0.57735,0.57735,0.57735;2.0944rad)
  Support = -> [YZ_Plane905]
  sketch-geometry (6):
    g0: LineSegment StartX=-1.9594 StartY=0.6 StartZ=0 EndX=-2.8094 EndY=0.6 EndZ=0
    g1: LineSegment StartX=-2.8094 StartY=0.6 StartZ=0 EndX=-2.8094 EndY=-0.6 EndZ=0
    g2: LineSegment StartX=-2.8094 StartY=-0.6 StartZ=0 EndX=-1.9594 EndY=-0.6 EndZ=0
    g3: LineSegment StartX=-1.9594 StartY=-0.6 StartZ=0 EndX=-2.3094 EndY=-0.4 EndZ=0
    g4: LineSegment StartX=-2.3094 StartY=-0.4 StartZ=0 EndX=-2.3094 EndY=0.4 EndZ=0
    g5: LineSegment StartX=-2.3094 StartY=0.4 StartZ=0 EndX=-1.9594 EndY=0.6 EndZ=0
  constraints (15):
    c: Horizontal(g0)
    c: Coincident(g0,g1)
    c: Coincident(g1,g2)
    c: Coincident(g2,g3)
    c: Coincident(g3,g4)
    c: Coincident(g4,g5)
    c: Coincident(g5,g0)
    c: Symmetric(g4,g3,g-1)
    c: Symmetric(g0,g2,g-1)
    c: Symmetric(g1,g0,g-1)
    c: DistanceX(g0,g4) = 0.5
    c: DistanceY(g3,g4) = 0.8
    c: DistanceY(g1,g0) = 1.2
    c: PointOnObject(g3,g-3)
    c: DistanceX(g4,g0) = 0.35
FEATURE [PartDesign::Groove] Groove210  label="M3 Nut Smooth202"
  Angle = 360
  Axis = (-2e-16,3e-16,1)
  Base = (0,0,0)
  BaseFeature = -> Pad1025
  Profile = -> Sketch2330
  ReferenceAxis = -> Sketch2330 [V_Axis]
  Reversed = true
FEATURE [PartDesign::Chamfer] Chamfer495  label="M3 Nut Smooth Hole202"
  Base = -> Groove210 [Edge24,Edge23]
  BaseFeature = -> Groove210
  Size = 0.2
FEATURE [PartDesign::Pocket] Pocket814  label="M3x8 Wrench151"
  BaseFeature = -> Pad1018
  Length = 1
  Length2 = 100
  Profile = -> Sketch2336
  Type = 0
FEATURE [PartDesign::Chamfer] Chamfer492  label="M3x8 Smooth147"
  Base = -> Pocket814 [Face11,Edge2,Edge24,Edge3]
  BaseFeature = -> Pocket814
  Size = 0.2
FEATURE [PartDesign::Pocket] Pocket815  label="M3x8 Wrench152"
  BaseFeature = -> Pad1020
  Length = 1
  Length2 = 100
  Profile = -> Sketch2271
  Type = 0
FEATURE [PartDesign::Chamfer] Chamfer496  label="M3x8 Smooth148"
  Base = -> Pocket815 [Face11,Edge2,Edge24,Edge3]
  BaseFeature = -> Pocket815
  Size = 0.2
FEATURE [PartDesign::Pad] Pad1026  label="M3x8 Thread151"
  BaseFeature = -> Pad1024
  Length = 8
  Length2 = 100
  Profile = -> Sketch2277
  Type = 0
FEATURE [Sketcher::SketchObject] Sketch2278
  MapMode = 5
  Placement = pos=(0,0,0) rot=(1,0,0;3.14159rad)
  Support = -> [Pad1026]
  sketch-geometry (7):
    g0: LineSegment StartX=0.77 StartY=0.44456 StartZ=0 EndX=0 EndY=0.889119 EndZ=0
    g1: LineSegment StartX=0 StartY=0.889119 StartZ=0 EndX=-0.77 EndY=0.44456 EndZ=0
    g2: LineSegment StartX=-0.77 StartY=0.44456 StartZ=0 EndX=-0.77 EndY=-0.44456 EndZ=0
    g3: LineSegment StartX=-0.77 StartY=-0.44456 StartZ=0 EndX=3.85628e-11 EndY=-0.889119 EndZ=0
    g4: LineSegment StartX=3.85628e-11 StartY=-0.889119 StartZ=0 EndX=0.77 EndY=-0.44456 EndZ=0
    g5: LineSegment StartX=0.77 StartY=-0.44456 StartZ=0 EndX=0.77 EndY=0.44456 EndZ=0
    g6: Circle [constr] CenterX=0 CenterY=0 CenterZ=0 NormalX=0 NormalY=0 NormalZ=1 AngleXU=0 Radius=0.889119
  constraints (16):
    c: Coincident(g0,g1)
    c: Coincident(g1,g2)
    c: Coincident(g2,g3)
    c: Coincident(g3,g4)
    c: Coincident(g4,g5)
    c: Coincident(g5,g0)
    c: Equal(g0, g1-g5) x5
    c: PointOnObject(g0,g6)
    c: PointOnObject(g1,g6)
    c: PointOnObject(g2,g6)
    c: PointOnObject(g3,g6)
    c: PointOnObject(g4,g6)
    c: PointOnObject(g5,g6)
    c: Coincident(g6,g-1)
    c: PointOnObject(g0,g-2)
    c: DistanceX(g1,g0) = 1.54
FEATURE [PartDesign::Pocket] Pocket809  label="M3x8 Wrench147"
  BaseFeature = -> Pad1026
  Length = 1
  Length2 = 100
  Profile = -> Sketch2278
  Type = 0
FEATURE [PartDesign::Chamfer] Chamfer489  label="M3x8 Smooth146"
  Base = -> Pocket809 [Face11,Edge2,Edge24,Edge3]
  BaseFeature = -> Pocket809
  Size = 0.2
FEATURE [PartDesign::Pad] Pad1027  label="M3x8 Thread152"
  BaseFeature = -> Pad1022
  Length = 8
  Length2 = 100
  Profile = -> Sketch2275
  Type = 0
FEATURE [Sketcher::SketchObject] Sketch2263
  MapMode = 5
  Placement = pos=(0,0,0) rot=(1,0,0;3.14159rad)
  Support = -> [Pad1027]
  sketch-geometry (7):
    g0: LineSegment StartX=0.77 StartY=0.44456 StartZ=0 EndX=0 EndY=0.889119 EndZ=0
    g1: LineSegment StartX=0 StartY=0.889119 StartZ=0 EndX=-0.77 EndY=0.44456 EndZ=0
    g2: LineSegment StartX=-0.77 StartY=0.44456 StartZ=0 EndX=-0.77 EndY=-0.44456 EndZ=0
    g3: LineSegment StartX=-0.77 StartY=-0.44456 StartZ=0 EndX=3.85628e-11 EndY=-0.889119 EndZ=0
    g4: LineSegment StartX=3.85628e-11 StartY=-0.889119 StartZ=0 EndX=0.77 EndY=-0.44456 EndZ=0
    g5: LineSegment StartX=0.77 StartY=-0.44456 StartZ=0 EndX=0.77 EndY=0.44456 EndZ=0
    g6: Circle [constr] CenterX=0 CenterY=0 CenterZ=0 NormalX=0 NormalY=0 NormalZ=1 AngleXU=0 Radius=0.889119
  constraints (16):
    c: Coincident(g0,g1)
    c: Coincident(g1,g2)
    c: Coincident(g2,g3)
    c: Coincident(g3,g4)
    c: Coincident(g4,g5)
    c: Coincident(g5,g0)
    c: Equal(g0, g1-g5) x5
    c: PointOnObject(g0,g6)
    c: PointOnObject(g1,g6)
    c: PointOnObject(g2,g6)
    c: PointOnObject(g3,g6)
    c: PointOnObject(g4,g6)
    c: PointOnObject(g5,g6)
    c: Coincident(g6,g-1)
    c: PointOnObject(g0,g-2)
    c: DistanceX(g1,g0) = 1.54
FEATURE [PartDesign::Pocket] Pocket813  label="M3x8 Wrench150"
  BaseFeature = -> Pad1027
  Length = 1
  Length2 = 100
  Profile = -> Sketch2263
  Type = 0
FEATURE [PartDesign::Chamfer] Chamfer497  label="M3x8 Smooth149"
  Base = -> Pocket813 [Face11,Edge2,Edge24,Edge3]
  BaseFeature = -> Pocket813
  Size = 0.2
FEATURE [PartDesign::Pad] Pad1028  label="M3 Nut Primitive202"
  Length = 0.6
  Length2 = 0.6
  Profile = -> Sketch2333
  Type = 4
FEATURE [Sketcher::SketchObject] Sketch2270
  ExternalGeometry = -> [Pad1028]
  MapMode = 5
  Placement = pos=(0,0,0) rot=(0.57735,0.57735,0.57735;2.0944rad)
  Support = -> [YZ_Plane903]
  sketch-geometry (6):
    g0: LineSegment StartX=-1.9594 StartY=0.6 StartZ=0 EndX=-2.8094 EndY=0.6 EndZ=0
    g1: LineSegment StartX=-2.8094 StartY=0.6 StartZ=0 EndX=-2.8094 EndY=-0.6 EndZ=0
    g2: LineSegment StartX=-2.8094 StartY=-0.6 StartZ=0 EndX=-1.9594 EndY=-0.6 EndZ=0
    g3: LineSegment StartX=-1.9594 StartY=-0.6 StartZ=0 EndX=-2.3094 EndY=-0.4 EndZ=0
    g4: LineSegment StartX=-2.3094 StartY=-0.4 StartZ=0 EndX=-2.3094 EndY=0.4 EndZ=0
    g5: LineSegment StartX=-2.3094 StartY=0.4 StartZ=0 EndX=-1.9594 EndY=0.6 EndZ=0
  constraints (15):
    c: Horizontal(g0)
    c: Coincident(g0,g1)
    c: Coincident(g1,g2)
    c: Coincident(g2,g3)
    c: Coincident(g3,g4)
    c: Coincident(g4,g5)
    c: Coincident(g5,g0)
    c: Symmetric(g4,g3,g-1)
    c: Symmetric(g0,g2,g-1)
    c: Symmetric(g1,g0,g-1)
    c: DistanceX(g0,g4) = 0.5
    c: DistanceY(g3,g4) = 0.8
    c: DistanceY(g1,g0) = 1.2
    c: PointOnObject(g3,g-3)
    c: DistanceX(g4,g0) = 0.35
FEATURE [PartDesign::Groove] Groove205  label="M3 Nut Smooth197"
  Angle = 360
  Axis = (-2e-16,3e-16,1)
  Base = (0,0,0)
  BaseFeature = -> Pad1028
  Profile = -> Sketch2270
  ReferenceAxis = -> Sketch2270 [V_Axis]
  Reversed = true
FEATURE [PartDesign::Chamfer] Chamfer487  label="M3 Nut Smooth Hole197"
  Base = -> Groove205 [Edge24,Edge23]
  BaseFeature = -> Groove205
  Size = 0.2
FEATURE [Sketcher::SketchObject] Sketch2341
  MapMode = 5
  Support = -> [XY_Plane940]
  sketch-geometry (8):
    g0: LineSegment StartX=-35 StartY=70 StartZ=0 EndX=35 EndY=70 EndZ=0
    g1: LineSegment StartX=55 StartY=50 StartZ=0 EndX=55 EndY=25 EndZ=0
    g2: LineSegment StartX=30 StartY=0 StartZ=0 EndX=-30 EndY=0 EndZ=0
    g3: LineSegment StartX=-55 StartY=25 StartZ=0 EndX=-55 EndY=50 EndZ=0
    g4: ArcOfCircle CenterX=-35 CenterY=50 CenterZ=0 NormalX=0 NormalY=0 NormalZ=1 AngleXU=0 Radius=20 StartAngle=1.5708 EndAngle=3.14159
    g5: ArcOfCircle CenterX=35 CenterY=50 CenterZ=0 NormalX=0 NormalY=0 NormalZ=1 AngleXU=0 Radius=20 StartAngle=0 EndAngle=1.5708
    g6: ArcOfCircle CenterX=30 CenterY=25 CenterZ=0 NormalX=0 NormalY=0 NormalZ=1 AngleXU=0 Radius=25 StartAngle=4.71239 EndAngle=6.28319
    g7: ArcOfCircle CenterX=-30 CenterY=25 CenterZ=0 NormalX=0 NormalY=0 NormalZ=1 AngleXU=0 Radius=25 StartAngle=3.14159 EndAngle=4.71239
  constraints (19):
    c: Horizontal(g0)
    c: Horizontal(g2)
    c: Vertical(g1)
    c: Vertical(g3)
    c: Tangent(g3,g4) = 1.5708
    c: Tangent(g0,g4) = 1.5708
    c: Tangent(g0,g5) = 1.5708
    c: Tangent(g1,g5) = 1.5708
    c: Tangent(g1,g6) = 1.5708
    c: Tangent(g2,g6) = 1.5708
    c: Tangent(g2,g7) = 1.5708
    c: Tangent(g3,g7) = 1.5708
    c: Equal(g4,g5)
    c: Equal(g7,g6)
    c: Symmetric(g2,g2,g-1)
    c: Radius(g4) = 20
    c: Radius(g7) = 25
    c: DistanceY(g2,g0) = 70
    c: DistanceX(g3,g1) = 110
FEATURE [PartDesign::Pad] Pad989  label="Baseplate039"
  Length = 5
  Length2 = 100
  Profile = -> Sketch2341
  Type = 0
FEATURE [Sketcher::SketchObject] Sketch2346
  MapMode = 5
  Placement = pos=(0,0,5) rot=(0,0,1;0rad)
  Support = -> [Pad989]
  sketch-geometry (8):
    g0: LineSegment StartX=-10 StartY=58 StartZ=0 EndX=10 EndY=58 EndZ=0
    g1: LineSegment StartX=20 StartY=48 StartZ=0 EndX=20 EndY=22 EndZ=0
    g2: LineSegment StartX=10 StartY=12 StartZ=0 EndX=-10 EndY=12 EndZ=0
    g3: LineSegment StartX=-20 StartY=22 StartZ=0 EndX=-20 EndY=48 EndZ=0
    g4: ArcOfCircle CenterX=-10 CenterY=48 CenterZ=0 NormalX=0 NormalY=0 NormalZ=1 AngleXU=0 Radius=10 StartAngle=1.5708 EndAngle=3.14159
    g5: ArcOfCircle CenterX=10 CenterY=48 CenterZ=0 NormalX=0 NormalY=0 NormalZ=1 AngleXU=0 Radius=10 StartAngle=2e-16 EndAngle=1.5708
    g6: ArcOfCircle CenterX=10 CenterY=22 CenterZ=0 NormalX=0 NormalY=0 NormalZ=1 AngleXU=0 Radius=10 StartAngle=4.71239 EndAngle=6.28319
    g7: ArcOfCircle CenterX=-10 CenterY=22 CenterZ=0 NormalX=0 NormalY=0 NormalZ=1 AngleXU=0 Radius=10 StartAngle=3.14159 EndAngle=4.71239
  constraints (19):
    c: Horizontal(g0)
    c: Vertical(g1)
    c: Vertical(g3)
    c: Tangent(g3,g4) = 1.5708
    c: Tangent(g0,g4) = 1.5708
    c: Tangent(g0,g5) = 1.5708
    c: Tangent(g1,g5) = 1.5708
    c: Tangent(g1,g6) = 1.5708
    c: Tangent(g2,g6) = 1.5708
    c: Tangent(g2,g7) = 1.5708
    c: Tangent(g3,g7) = 1.5708
    c: Equal(g5,g4)
    c: Equal(g4,g7)
    c: Equal(g7,g6)
    c: Symmetric(g2,g2,g-2)
    c: DistanceX(g3,g1) = 40
    c: DistanceY(g-1,g2) = 12
    c: DistanceY(g2,g0) = 46
    c: Radius(g5) = 10
FEATURE [PartDesign::Pocket] Pocket798  label="Accesshole005"
  BaseFeature = -> Pad989
  Length = 5
  Length2 = 100
  Profile = -> Sketch2346
  Type = 0
FEATURE [Sketcher::SketchObject] Sketch2342
  MapMode = 5
  Placement = pos=(0,0,5) rot=(0,0,1;0rad)
  Support = -> [Pocket798]
  sketch-geometry (4):
    g0: Circle CenterX=-5 CenterY=6 CenterZ=0 NormalX=0 NormalY=0 NormalZ=1 AngleXU=0 Radius=1.6
    g1: Circle CenterX=5 CenterY=6 CenterZ=0 NormalX=0 NormalY=0 NormalZ=1 AngleXU=0 Radius=1.6
    g2: Circle CenterX=15 CenterY=64 CenterZ=0 NormalX=0 NormalY=0 NormalZ=1 AngleXU=0 Radius=1.6
    g3: Circle CenterX=-15 CenterY=64 CenterZ=0 NormalX=0 NormalY=0 NormalZ=1 AngleXU=0 Radius=1.6
  constraints (10):
    c: Symmetric(g0,g1,g-2)
    c: Symmetric(g3,g2,g-2)
    c: DistanceX(g3,g2) = 30
    c: DistanceX(g0,g1) = 10
    c: DistanceY(g-1,g0) = 6
    c: DistanceY(g-1,g2) = 64
    c: Radius(g1) = 1.6
    c: Equal(g2,g3)
    c: Equal(g3,g0)
    c: Equal(g0,g1)
FEATURE [PartDesign::Pocket] Pocket794  label="Screwholes009"
  BaseFeature = -> Pocket798
  Length = 5
  Length2 = 100
  Profile = -> Sketch2342
  Type = 0
FEATURE [Sketcher::SketchObject] Sketch2344
  ExternalGeometry = -> [Pocket794]
  MapMode = 5
  Placement = pos=(0,0,5) rot=(0,0,1;0rad)
  Support = -> [Pocket794]
  sketch-geometry (4):
    g0: Circle CenterX=-15 CenterY=64 CenterZ=0 NormalX=0 NormalY=0 NormalZ=1 AngleXU=0 Radius=3
    g1: Circle CenterX=15 CenterY=64 CenterZ=0 NormalX=0 NormalY=0 NormalZ=1 AngleXU=0 Radius=3
    g2: Circle CenterX=-5 CenterY=6 CenterZ=0 NormalX=0 NormalY=0 NormalZ=1 AngleXU=0 Radius=3
    g3: Circle CenterX=5 CenterY=6 CenterZ=0 NormalX=0 NormalY=0 NormalZ=1 AngleXU=0 Radius=3
  constraints (8):
    c: Coincident(g0,g-3)
    c: Coincident(g1,g-4)
    c: Coincident(g2,g-5)
    c: Coincident(g3,g-6)
    c: Equal(g3,g2)
    c: Equal(g2,g0)
    c: Equal(g0,g1)
    c: Radius(g1) = 3
FEATURE [PartDesign::Pocket] Pocket796  label="Screwheads001"
  BaseFeature = -> Pocket794
  Length = 3
  Length2 = 100
  Profile = -> Sketch2344
  Type = 0
FEATURE [Sketcher::SketchObject] Sketch2343
  MapMode = 5
  Placement = pos=(0,0,5) rot=(0,0,1;0rad)
  Support = -> [Pocket796]
  sketch-geometry (2):
    g0: Circle CenterX=-39 CenterY=44 CenterZ=0 NormalX=0 NormalY=0 NormalZ=1 AngleXU=0 Radius=6.15
    g1: Circle CenterX=39 CenterY=44 CenterZ=0 NormalX=0 NormalY=0 NormalZ=1 AngleXU=0 Radius=6.15
  constraints (5):
    c: Equal(g1,g0)
    c: Symmetric(g0,g1,g-2)
    c: DistanceX(g0,g1) = 78
    c: DistanceY(g-1,g0) = 44
    c: Radius(g0) = 6.15
FEATURE [PartDesign::Pocket] Pocket792  label="Servohorn Axis005"
  BaseFeature = -> Pocket796
  Length = 5
  Length2 = 100
  Profile = -> Sketch2343
  Type = 0
FEATURE [Sketcher::SketchObject] Sketch2347
  ExternalGeometry = -> [Pocket792]
  MapMode = 5
  Placement = pos=(0,0,5) rot=(0,0,1;0rad)
  Support = -> [Pocket792]
  sketch-geometry (64):
    g0: LineSegment [constr] StartX=-39 StartY=57.5 StartZ=0 EndX=-50.6913 EndY=50.75 EndZ=0
    g1: LineSegment [constr] StartX=-50.6913 StartY=50.75 StartZ=0 EndX=-50.6913 EndY=37.25 EndZ=0
    g2: LineSegment [constr] StartX=-50.6913 StartY=37.25 StartZ=0 EndX=-39 EndY=30.5 EndZ=0
    g3: LineSegment [constr] StartX=-39 StartY=30.5 StartZ=0 EndX=-27.3087 EndY=37.25 EndZ=0
    g4: LineSegment [constr] StartX=-27.3087 StartY=37.25 StartZ=0 EndX=-27.3087 EndY=50.75 EndZ=0
    g5: LineSegment [constr] StartX=-27.3087 StartY=50.75 StartZ=0 EndX=-39 EndY=57.5 EndZ=0
    g6: Circle [constr] CenterX=-39 CenterY=44 CenterZ=0 NormalX=0 NormalY=0 NormalZ=1 AngleXU=0 Radius=13.5
    g7: LineSegment [constr] StartX=39 StartY=57.5 StartZ=0 EndX=27.3087 EndY=50.75 EndZ=0
    g8: LineSegment [constr] StartX=27.3087 StartY=50.75 StartZ=0 EndX=27.3087 EndY=37.25 EndZ=0
    g9: LineSegment [constr] StartX=27.3087 StartY=37.25 StartZ=0 EndX=39 EndY=30.5 EndZ=0
    g10: LineSegment [constr] StartX=39 StartY=30.5 StartZ=0 EndX=50.6913 EndY=37.25 EndZ=0
    g11: LineSegment [constr] StartX=50.6913 StartY=37.25 StartZ=0 EndX=50.6913 EndY=50.75 EndZ=0
    g12: LineSegment [constr] StartX=50.6913 StartY=50.75 StartZ=0 EndX=39 EndY=57.5 EndZ=0
    g13: Circle [constr] CenterX=39 CenterY=44 CenterZ=0 NormalX=0 NormalY=0 NormalZ=1 AngleXU=0 Radius=13.5
    g14: ArcOfCircle CenterX=-39 CenterY=57.5 CenterZ=0 NormalX=0 NormalY=0 NormalZ=1 AngleXU=0 Radius=2.6 StartAngle=0.15815 EndAngle=2.98344
    g15: ArcOfCircle CenterX=-27.3087 CenterY=50.75 CenterZ=0 NormalX=0 NormalY=0 NormalZ=1 AngleXU=0 Radius=2.6 StartAngle=5.39414 EndAngle=8.21943
    g16: ArcOfCircle CenterX=-27.3087 CenterY=37.25 CenterZ=0 NormalX=0 NormalY=0 NormalZ=1 AngleXU=0 Radius=2.6 StartAngle=4.34694 EndAngle=7.17223
    g17: ArcOfCircle CenterX=-39 CenterY=30.5 CenterZ=0 NormalX=0 NormalY=0 NormalZ=1 AngleXU=0 Radius=2.6 StartAngle=3.29974 EndAngle=6.12503
    g18: ArcOfCircle CenterX=-50.6913 CenterY=37.25 CenterZ=0 NormalX=0 NormalY=0 NormalZ=1 AngleXU=0 Radius=2.6 StartAngle=2.25255 EndAngle=5.07784
    g19: ArcOfCircle CenterX=-50.6913 CenterY=50.75 CenterZ=0 NormalX=0 NormalY=0 NormalZ=1 AngleXU=0 Radius=2.6 StartAngle=1.20535 EndAngle=4.03064
    g20: ArcOfCircle CenterX=39 CenterY=57.5 CenterZ=0 NormalX=0 NormalY=0 NormalZ=1 AngleXU=0 Radius=2.6 StartAngle=0.15815 EndAngle=2.98344
    g21: ArcOfCircle CenterX=50.6913 CenterY=50.75 CenterZ=0 NormalX=0 NormalY=0 NormalZ=1 AngleXU=0 Radius=2.6 StartAngle=5.39414 EndAngle=8.21943
    g22: ArcOfCircle CenterX=50.6913 CenterY=37.25 CenterZ=0 NormalX=0 NormalY=0 NormalZ=1 AngleXU=0 Radius=2.6 StartAngle=4.34694 EndAngle=7.17223
    g23: ArcOfCircle CenterX=39 CenterY=30.5 CenterZ=0 NormalX=0 NormalY=0 NormalZ=1 AngleXU=0 Radius=2.6 StartAngle=3.29974 EndAngle=6.12503
    g24: ArcOfCircle CenterX=27.3087 CenterY=37.25 CenterZ=0 NormalX=0 NormalY=0 NormalZ=1 AngleXU=0 Radius=2.6 StartAngle=2.25255 EndAngle=5.07784
    g25: ArcOfCircle CenterX=27.3087 CenterY=50.75 CenterZ=0 NormalX=0 NormalY=0 NormalZ=1 AngleXU=0 Radius=2.6 StartAngle=1.20535 EndAngle=4.03064
    g26: LineSegment [constr] StartX=-42.75 StartY=50.4952 StartZ=0 EndX=-46.5 EndY=44 EndZ=0
    g27: LineSegment [constr] StartX=-46.5 StartY=44 StartZ=0 EndX=-42.75 EndY=37.5048 EndZ=0
    g28: LineSegment [constr] StartX=-42.75 StartY=37.5048 StartZ=0 EndX=-35.25 EndY=37.5048 EndZ=0
    g29: LineSegment [constr] StartX=-35.25 StartY=37.5048 StartZ=0 EndX=-31.5 EndY=44 EndZ=0
    g30: LineSegment [constr] StartX=-31.5 StartY=44 StartZ=0 EndX=-35.25 EndY=50.4952 EndZ=0
    g31: LineSegment [constr] StartX=-35.25 StartY=50.4952 StartZ=0 EndX=-42.75 EndY=50.4952 EndZ=0
    g32: Circle [constr] CenterX=-39 CenterY=44 CenterZ=0 NormalX=0 NormalY=0 NormalZ=1 AngleXU=0 Radius=7.5
    g33: LineSegment [constr] StartX=42.75 StartY=50.4952 StartZ=0 EndX=35.25 EndY=50.4952 EndZ=0
    g34: LineSegment [constr] StartX=35.25 StartY=50.4952 StartZ=0 EndX=31.5 EndY=44 EndZ=0
    g35: LineSegment [constr] StartX=31.5 StartY=44 StartZ=0 EndX=35.25 EndY=37.5048 EndZ=0
    g36: LineSegment [constr] StartX=35.25 StartY=37.5048 StartZ=0 EndX=42.75 EndY=37.5048 EndZ=0
    g37: LineSegment [constr] StartX=42.75 StartY=37.5048 StartZ=0 EndX=46.5 EndY=44 EndZ=0
    g38: LineSegment [constr] StartX=46.5 StartY=44 StartZ=0 EndX=42.75 EndY=50.4952 EndZ=0
    g39: Circle [constr] CenterX=39 CenterY=44 CenterZ=0 NormalX=0 NormalY=0 NormalZ=1 AngleXU=0 Radius=7.5
    g40: LineSegment StartX=-49.7622 StartY=53.1783 StartZ=0 EndX=-42.75 EndY=50.4952 EndZ=0
    g41: LineSegment StartX=-41.5676 StartY=57.9095 StartZ=0 EndX=-42.75 EndY=50.4952 EndZ=0
    g42: LineSegment StartX=-36.4324 StartY=57.9095 StartZ=0 EndX=-35.25 EndY=50.4952 EndZ=0
    g43: LineSegment StartX=-35.25 StartY=50.4952 StartZ=0 EndX=-28.2378 EndY=53.1783 EndZ=0
    g44: LineSegment StartX=-25.6703 StartY=48.7312 StartZ=0 EndX=-31.5 EndY=44 EndZ=0
    g45: LineSegment StartX=-31.5 StartY=44 StartZ=0 EndX=-25.6703 EndY=39.2688 EndZ=0
    g46: LineSegment StartX=-28.2378 StartY=34.8217 StartZ=0 EndX=-35.25 EndY=37.5048 EndZ=0
    g47: LineSegment StartX=-35.25 StartY=37.5048 StartZ=0 EndX=-36.4324 EndY=30.0905 EndZ=0
    g48: LineSegment StartX=-41.5676 StartY=30.0905 StartZ=0 EndX=-42.75 EndY=37.5048 EndZ=0
    g49: LineSegment StartX=-42.75 StartY=37.5048 StartZ=0 EndX=-49.7622 EndY=34.8217 EndZ=0
    g50: LineSegment StartX=-52.3297 StartY=39.2688 StartZ=0 EndX=-46.5 EndY=44 EndZ=0
    g51: LineSegment StartX=-46.5 StartY=44 StartZ=0 EndX=-52.3297 EndY=48.7312 EndZ=0
    g52: LineSegment StartX=25.6703 StartY=48.7312 StartZ=0 EndX=31.5 EndY=44 EndZ=0
    g53: LineSegment StartX=31.5 StartY=44 StartZ=0 EndX=25.6703 EndY=39.2688 EndZ=0
    g54: LineSegment StartX=28.2378 StartY=34.8217 StartZ=0 EndX=35.25 EndY=37.5048 EndZ=0
    g55: LineSegment StartX=35.25 StartY=37.5048 StartZ=0 EndX=36.4324 EndY=30.0905 EndZ=0
    g56: LineSegment StartX=41.5676 StartY=30.0905 StartZ=0 EndX=42.75 EndY=37.5048 EndZ=0
    g57: LineSegment StartX=42.75 StartY=37.5048 StartZ=0 EndX=49.7622 EndY=34.8217 EndZ=0
    g58: LineSegment StartX=52.3297 StartY=39.2688 StartZ=0 EndX=46.5 EndY=44 EndZ=0
    g59: LineSegment StartX=46.5 StartY=44 StartZ=0 EndX=52.3297 EndY=48.7312 EndZ=0
    g60: LineSegment StartX=49.7622 StartY=53.1783 StartZ=0 EndX=42.75 EndY=50.4952 EndZ=0
    g61: LineSegment StartX=42.75 StartY=50.4952 StartZ=0 EndX=41.5676 EndY=57.9095 EndZ=0
    g62: LineSegment StartX=36.4324 StartY=57.9095 StartZ=0 EndX=35.25 EndY=50.4952 EndZ=0
    g63: LineSegment StartX=35.25 StartY=50.4952 StartZ=0 EndX=28.2378 EndY=53.1783 EndZ=0
  constraints (127):
    c: Coincident(g0,g1)
    c: Coincident(g1,g2)
    c: Coincident(g2,g3)
    c: Coincident(g3,g4)
    c: Coincident(g4,g5)
    c: Coincident(g5,g0)
    c: Equal(g0, g1-g5) x5
    c: PointOnObject(g0,g6)
    c: PointOnObject(g1,g6)
    c: PointOnObject(g2,g6)
    c: PointOnObject(g3,g6)
    c: PointOnObject(g4,g6)
    c: PointOnObject(g5,g6)
    c: Coincident(g7,g8)
    c: Coincident(g8,g9)
    c: Coincident(g9,g10)
    c: Coincident(g10,g11)
    c: Coincident(g11,g12)
    c: Coincident(g12,g7)
    c: Equal(g7, g8-g12) x5
    c: PointOnObject(g7,g13)
    c: PointOnObject(g8,g13)
    c: PointOnObject(g9,g13)
    c: PointOnObject(g10,g13)
    c: PointOnObject(g11,g13)
    c: PointOnObject(g12,g13)
    c: Coincident(g13,g-4)
    c: Coincident(g6,g-3)
    c: Equal(g6,g13)
    c: Vertical(g8)
    c: Vertical(g4)
    c: Radius(g6) = 13.5
    c: Coincident(g26,g27)
    c: Coincident(g27,g28)
    c: Coincident(g28,g29)
    c: Coincident(g29,g30)
    c: Coincident(g30,g31)
    c: Coincident(g31,g26)
    c: Equal(g26, g27-g31) x5
    c: PointOnObject(g26,g32)
    c: PointOnObject(g27,g32)
    c: PointOnObject(g28,g32)
    c: PointOnObject(g29,g32)
    c: PointOnObject(g30,g32)
    c: PointOnObject(g31,g32)
    c: Coincident(g32,g6)
    c: Coincident(g33,g34)
    c: Coincident(g34,g35)
    c: Coincident(g35,g36)
    c: Coincident(g36,g37)
    c: Coincident(g37,g38)
    c: Coincident(g38,g33)
    c: Equal(g33, g34-g38) x5
    c: PointOnObject(g33,g39)
    c: PointOnObject(g34,g39)
    c: PointOnObject(g35,g39)
    c: PointOnObject(g36,g39)
    c: PointOnObject(g37,g39)
    c: PointOnObject(g38,g39)
    c: Coincident(g13,g39)
    c: Equal(g32,g39)
    c: Radius(g39) = 7.5
    c: Horizontal(g31)
    c: Horizontal(g33)
    c: Coincident(g40,g26)
    c: Coincident(g41,g40)
    c: Coincident(g42,g30)
    c: Coincident(g43,g42)
    c: Coincident(g44,g29)
    c: Coincident(g45,g44)
    c: Coincident(g46,g28)
    c: Coincident(g47,g46)
    c: Coincident(g48,g27)
    c: Coincident(g49,g48)
    c: Coincident(g50,g26)
    c: Coincident(g51,g50)
    c: Coincident(g52,g34)
    c: Coincident(g53,g52)
    c: Coincident(g54,g35)
    c: Coincident(g55,g54)
    c: Coincident(g56,g36)
    c: Coincident(g57,g56)
    c: Coincident(g58,g37)
    c: Coincident(g59,g58)
    c: Coincident(g60,g33)
    c: Coincident(g61,g60)
    c: Coincident(g62,g33)
    c: Coincident(g63,g62)
    c: Radius(g19) = 2.6
    c: Equal(g19, g14-g18) x5
    c: Equal(g19, g20-g25) x6
    c: Tangent(g42,g14) = 1.5708
    c: Tangent(g43,g15) = 1.5708
    c: Tangent(g44,g15) = 1.5708
    c: Tangent(g45,g16) = 1.5708
    c: Tangent(g46,g16) = 1.5708
    c: Tangent(g47,g17) = 1.5708
    c: Tangent(g48,g17) = 1.5708
    c: Tangent(g49,g18) = 1.5708
    c: Tangent(g50,g18) = 1.5708
    c: Tangent(g51,g19) = 1.5708
    c: Tangent(g40,g19) = 1.5708
    c: Tangent(g41,g14) = -1.5708
    c: Tangent(g61,g20) = -1.5708
    c: Tangent(g60,g21) = -1.5708
    c: Tangent(g59,g21) = -1.5708
    c: Tangent(g58,g22) = -1.5708
    c: Tangent(g57,g22) = -1.5708
    c: Tangent(g56,g23) = -1.5708
    c: Tangent(g55,g23) = -1.5708
    c: Tangent(g54,g24) = -1.5708
    c: Tangent(g53,g24) = -1.5708
    c: Tangent(g52,g25) = -1.5708
    c: Tangent(g63,g25) = -1.5708
    c: Tangent(g62,g20) = -1.5708
    c: Coincident(g20,g7)
    c: Coincident(g21,g11)
    c: Coincident(g22,g10)
    c: Coincident(g23,g9)
    c: Coincident(g24,g8)
    c: Coincident(g25,g7)
    c: Coincident(g14,g0)
    c: Coincident(g15,g4)
    c: Coincident(g16,g3)
    c: Coincident(g17,g2)
    c: Coincident(g18,g1)
    c: Coincident(g19,g0)
FEATURE [PartDesign::Pocket] Pocket797  label="Servohorn Mount001"
  BaseFeature = -> Pocket792
  Length = 2
  Length2 = 100
  Profile = -> Sketch2347
  Type = 0
FEATURE [Sketcher::SketchObject] Sketch2345
  ExternalGeometry = -> [Pocket797]
  MapMode = 5
  Placement = pos=(0,0,3) rot=(0,0,1;0rad)
  Support = -> [Pocket797]
  sketch-geometry (26):
    g0: LineSegment [constr] StartX=-39 StartY=54.5 StartZ=0 EndX=-48.0933 EndY=49.25 EndZ=0
    g1: LineSegment [constr] StartX=-48.0933 StartY=49.25 StartZ=0 EndX=-48.0933 EndY=38.75 EndZ=0
    g2: LineSegment [constr] StartX=-48.0933 StartY=38.75 StartZ=0 EndX=-39 EndY=33.5 EndZ=0
    g3: LineSegment [constr] StartX=-39 StartY=33.5 StartZ=0 EndX=-29.9067 EndY=38.75 EndZ=0
    g4: LineSegment [constr] StartX=-29.9067 StartY=38.75 StartZ=0 EndX=-29.9067 EndY=49.25 EndZ=0
    g5: LineSegment [constr] StartX=-29.9067 StartY=49.25 StartZ=0 EndX=-39 EndY=54.5 EndZ=0
    g6: Circle [constr] CenterX=-39 CenterY=44 CenterZ=0 NormalX=0 NormalY=0 NormalZ=1 AngleXU=0 Radius=10.5
    g7: LineSegment [constr] StartX=39 StartY=54.5 StartZ=0 EndX=29.9067 EndY=49.25 EndZ=0
    g8: LineSegment [constr] StartX=29.9067 StartY=49.25 StartZ=0 EndX=29.9067 EndY=38.75 EndZ=0
    g9: LineSegment [constr] StartX=29.9067 StartY=38.75 StartZ=0 EndX=39 EndY=33.5 EndZ=0
    g10: LineSegment [constr] StartX=39 StartY=33.5 StartZ=0 EndX=48.0933 EndY=38.75 EndZ=0
    g11: LineSegment [constr] StartX=48.0933 StartY=38.75 StartZ=0 EndX=48.0933 EndY=49.25 EndZ=0
    g12: LineSegment [constr] StartX=48.0933 StartY=49.25 StartZ=0 EndX=39 EndY=54.5 EndZ=0
    g13: Circle [constr] CenterX=39 CenterY=44 CenterZ=0 NormalX=0 NormalY=0 NormalZ=1 AngleXU=0 Radius=10.5
    g14: Circle CenterX=-39 CenterY=54.5 CenterZ=0 NormalX=0 NormalY=0 NormalZ=1 AngleXU=0 Radius=0.95
    g15: Circle CenterX=-29.9067 CenterY=49.25 CenterZ=0 NormalX=0 NormalY=0 NormalZ=1 AngleXU=0 Radius=0.95
    g16: Circle CenterX=-29.9067 CenterY=38.75 CenterZ=0 NormalX=0 NormalY=0 NormalZ=1 AngleXU=0 Radius=0.95
    g17: Circle CenterX=-39 CenterY=33.5 CenterZ=0 NormalX=0 NormalY=0 NormalZ=1 AngleXU=0 Radius=0.95
    g18: Circle CenterX=-48.0933 CenterY=38.75 CenterZ=0 NormalX=0 NormalY=0 NormalZ=1 AngleXU=0 Radius=0.95
    g19: Circle CenterX=-48.0933 CenterY=49.25 CenterZ=0 NormalX=0 NormalY=0 NormalZ=1 AngleXU=0 Radius=0.95
    g20: Circle CenterX=29.9067 CenterY=49.25 CenterZ=0 NormalX=0 NormalY=0 NormalZ=1 AngleXU=0 Radius=0.95
    g21: Circle CenterX=39 CenterY=54.5 CenterZ=0 NormalX=0 NormalY=0 NormalZ=1 AngleXU=0 Radius=0.95
    g22: Circle CenterX=48.0933 CenterY=49.25 CenterZ=0 NormalX=0 NormalY=0 NormalZ=1 AngleXU=0 Radius=0.95
    g23: Circle CenterX=48.0933 CenterY=38.75 CenterZ=0 NormalX=0 NormalY=0 NormalZ=1 AngleXU=0 Radius=0.95
    g24: Circle CenterX=39 CenterY=33.5 CenterZ=0 NormalX=0 NormalY=0 NormalZ=1 AngleXU=0 Radius=0.95
    g25: Circle CenterX=29.9067 CenterY=38.75 CenterZ=0 NormalX=0 NormalY=0 NormalZ=1 AngleXU=0 Radius=0.95
  constraints (48):
    c: Coincident(g0,g1)
    c: Coincident(g1,g2)
    c: Coincident(g2,g3)
    c: Coincident(g3,g4)
    c: Coincident(g4,g5)
    c: Coincident(g5,g0)
    c: Equal(g0, g1-g5) x5
    c: PointOnObject(g0,g6)
    c: PointOnObject(g1,g6)
    c: PointOnObject(g2,g6)
    c: PointOnObject(g3,g6)
    c: PointOnObject(g4,g6)
    c: PointOnObject(g5,g6)
    c: Coincident(g6,g-3)
    c: Coincident(g7,g8)
    c: Coincident(g8,g9)
    c: Coincident(g9,g10)
    c: Coincident(g10,g11)
    c: Coincident(g11,g12)
    c: Coincident(g12,g7)
    c: Equal(g7, g8-g12) x5
    c: PointOnObject(g7,g13)
    c: PointOnObject(g8,g13)
    c: PointOnObject(g9,g13)
    c: PointOnObject(g10,g13)
    c: PointOnObject(g11,g13)
    c: PointOnObject(g12,g13)
    c: Coincident(g13,g-4)
    c: Vertical(g4)
    c: Vertical(g8)
    c: Equal(g13,g6)
    c: Radius(g6) = 10.5
    c: Coincident(g14,g0)
    c: Coincident(g15,g4)
    c: Coincident(g16,g3)
    c: Coincident(g17,g2)
    c: Coincident(g18,g1)
    c: Coincident(g19,g0)
    c: Coincident(g20,g7)
    c: Coincident(g21,g7)
    c: Coincident(g22,g11)
    c: Coincident(g23,g10)
    c: Coincident(g24,g9)
    c: Coincident(g25,g8)
    c: Radius(g20) = 0.95
    c: Equal(g20, g21-g25) x5
    c: Equal(g20, g15-g19) x5
    c: Equal(g20,g14)
FEATURE [PartDesign::Pocket] Pocket793  label="Servohorn Screws001"
  BaseFeature = -> Pocket797
  Length = 3
  Length2 = 100
  Profile = -> Sketch2345
  Type = 0
FEATURE [PartDesign::Fillet] Fillet252  label="Servohorn Fillet001"
  Base = -> Pocket793 [Edge214,Edge184,Edge190,Edge208,Edge174,Edge143,Edge168,Edge150,Edge202,Edge196,Edge162,Edge156]
  BaseFeature = -> Pocket793
  Radius = 1
FEATURE [Sketcher::SketchObject] Sketch2351
  MapMode = 5
  Support = -> [XY_Plane913]
  sketch-geometry (64):
    g0: LineSegment [constr] StartX=-3.75 StartY=6.49519 StartZ=0 EndX=-7.5 EndY=0 EndZ=0
    g1: LineSegment [constr] StartX=-7.5 StartY=0 StartZ=0 EndX=-3.75 EndY=-6.49519 EndZ=0
    g2: LineSegment [constr] StartX=-3.75 StartY=-6.49519 StartZ=0 EndX=3.75 EndY=-6.49519 EndZ=0
    g3: LineSegment [constr] StartX=3.75 StartY=-6.49519 StartZ=0 EndX=7.5 EndY=0 EndZ=0
    g4: LineSegment [constr] StartX=7.5 StartY=0 StartZ=0 EndX=3.75 EndY=6.49519 EndZ=0
    g5: LineSegment [constr] StartX=3.75 StartY=6.49519 StartZ=0 EndX=-3.75 EndY=6.49519 EndZ=0
    g6: Circle [constr] CenterX=0 CenterY=0 CenterZ=0 NormalX=0 NormalY=0 NormalZ=1 AngleXU=0 Radius=7.5
    g7: LineSegment [constr] StartX=0 StartY=7.5 StartZ=0 EndX=-6.49519 EndY=3.75 EndZ=0
    g8: LineSegment [constr] StartX=-6.49519 StartY=3.75 StartZ=0 EndX=-6.49519 EndY=-3.75 EndZ=0
    g9: LineSegment [constr] StartX=-6.49519 StartY=-3.75 StartZ=0 EndX=9.8e-15 EndY=-7.5 EndZ=0
    g10: LineSegment [constr] StartX=9.8e-15 StartY=-7.5 StartZ=0 EndX=6.49519 EndY=-3.75 EndZ=0
    g11: LineSegment [constr] StartX=6.49519 StartY=-3.75 StartZ=0 EndX=6.49519 EndY=3.75 EndZ=0
    g12: LineSegment [constr] StartX=6.49519 StartY=3.75 StartZ=0 EndX=0 EndY=7.5 EndZ=0
    g13: Circle [constr] CenterX=0 CenterY=0 CenterZ=0 NormalX=0 NormalY=0 NormalZ=1 AngleXU=0 Radius=7.5
    g14: LineSegment [constr] StartX=0 StartY=10.5 StartZ=0 EndX=-9.09327 EndY=5.25 EndZ=0
    g15: LineSegment [constr] StartX=-9.09327 StartY=5.25 StartZ=0 EndX=-9.09327 EndY=-5.25 EndZ=0
    g16: LineSegment [constr] StartX=-9.09327 StartY=-5.25 StartZ=0 EndX=-1.42e-14 EndY=-10.5 EndZ=0
    g17: LineSegment [constr] StartX=-1.42e-14 StartY=-10.5 StartZ=0 EndX=9.09327 EndY=-5.25 EndZ=0
    g18: LineSegment [constr] StartX=9.09327 StartY=-5.25 StartZ=0 EndX=9.09327 EndY=5.25 EndZ=0
    g19: LineSegment [constr] StartX=9.09327 StartY=5.25 StartZ=0 EndX=0 EndY=10.5 EndZ=0
    g20: Circle [constr] CenterX=0 CenterY=0 CenterZ=0 NormalX=0 NormalY=0 NormalZ=1 AngleXU=0 Radius=10.5
    g21: LineSegment [constr] StartX=0 StartY=13.5 StartZ=0 EndX=-11.6913 EndY=6.75 EndZ=0
    g22: LineSegment [constr] StartX=-11.6913 StartY=6.75 StartZ=0 EndX=-11.6913 EndY=-6.75 EndZ=0
    g23: LineSegment [constr] StartX=-11.6913 StartY=-6.75 StartZ=0 EndX=0 EndY=-13.5 EndZ=0
    g24: LineSegment [constr] StartX=0 StartY=-13.5 StartZ=0 EndX=11.6913 EndY=-6.75 EndZ=0
    g25: LineSegment [constr] StartX=11.6913 StartY=-6.75 StartZ=0 EndX=11.6913 EndY=6.75 EndZ=0
    g26: LineSegment [constr] StartX=11.6913 StartY=6.75 StartZ=0 EndX=0 EndY=13.5 EndZ=0
    g27: Circle [constr] CenterX=0 CenterY=0 CenterZ=0 NormalX=0 NormalY=0 NormalZ=1 AngleXU=0 Radius=13.5
    g28: ArcOfCircle CenterX=0 CenterY=13.5 CenterZ=0 NormalX=0 NormalY=0 NormalZ=1 AngleXU=0 Radius=2.5 StartAngle=0.171439 EndAngle=2.97015
    g29: ArcOfCircle CenterX=11.6913 CenterY=6.75 CenterZ=0 NormalX=0 NormalY=0 NormalZ=1 AngleXU=0 Radius=2.5 StartAngle=5.40743 EndAngle=8.20614
    g30: ArcOfCircle CenterX=11.6913 CenterY=-6.75 CenterZ=0 NormalX=0 NormalY=0 NormalZ=1 AngleXU=0 Radius=2.5 StartAngle=4.36023 EndAngle=7.15894
    g31: ArcOfCircle CenterX=0 CenterY=-13.5 CenterZ=0 NormalX=0 NormalY=0 NormalZ=1 AngleXU=0 Radius=2.5 StartAngle=3.31303 EndAngle=6.11175
    g32: ArcOfCircle CenterX=-11.6913 CenterY=-6.75 CenterZ=0 NormalX=0 NormalY=0 NormalZ=1 AngleXU=0 Radius=2.5 StartAngle=2.26583 EndAngle=5.06455
    g33: ArcOfCircle CenterX=-11.6913 CenterY=6.75 CenterZ=0 NormalX=0 NormalY=0 NormalZ=1 AngleXU=0 Radius=2.5 StartAngle=1.21864 EndAngle=4.01735
    g34: LineSegment StartX=-10.829 StartY=9.09658 StartZ=0 EndX=-3.75 EndY=6.49519 EndZ=0
    g35: LineSegment StartX=-3.75 StartY=6.49519 StartZ=0 EndX=-2.46335 EndY=13.9265 EndZ=0
    g36: LineSegment StartX=2.46335 StartY=13.9265 StartZ=0 EndX=3.75 EndY=6.49519 EndZ=0
    g37: LineSegment StartX=3.75 StartY=6.49519 StartZ=0 EndX=10.829 EndY=9.09658 EndZ=0
    g38: LineSegment StartX=13.2924 StartY=4.82993 StartZ=0 EndX=7.5 EndY=0 EndZ=0
    g39: LineSegment StartX=7.5 StartY=0 StartZ=0 EndX=13.2924 EndY=-4.82993 EndZ=0
    g40: LineSegment StartX=10.829 StartY=-9.09658 StartZ=0 EndX=3.75 EndY=-6.49519 EndZ=0
    g41: LineSegment StartX=3.75 StartY=-6.49519 StartZ=0 EndX=2.46335 EndY=-13.9265 EndZ=0
    g42: LineSegment StartX=-2.46335 StartY=-13.9265 StartZ=0 EndX=-3.75 EndY=-6.49519 EndZ=0
    g43: LineSegment StartX=-3.75 StartY=-6.49519 StartZ=0 EndX=-10.829 EndY=-9.09658 EndZ=0
    g44: LineSegment StartX=-13.2924 StartY=-4.82993 StartZ=0 EndX=-7.5 EndY=0 EndZ=0
    g45: LineSegment StartX=-7.5 StartY=0 StartZ=0 EndX=-13.2924 EndY=4.82993 EndZ=0
    g46: Circle CenterX=-11.6913 CenterY=6.75 CenterZ=0 NormalX=0 NormalY=0 NormalZ=1 AngleXU=0 Radius=0.75
    g47: Circle CenterX=-9.09327 CenterY=5.25 CenterZ=0 NormalX=0 NormalY=0 NormalZ=1 AngleXU=0 Radius=0.75
    g48: Circle CenterX=-6.49519 CenterY=3.75 CenterZ=0 NormalX=0 NormalY=0 NormalZ=1 AngleXU=0 Radius=0.75
    g49: Circle CenterX=0 CenterY=13.5 CenterZ=0 NormalX=0 NormalY=0 NormalZ=1 AngleXU=0 Radius=0.75
    g50: Circle CenterX=0 CenterY=10.5 CenterZ=0 NormalX=0 NormalY=0 NormalZ=1 AngleXU=0 Radius=0.75
    g51: Circle CenterX=0 CenterY=7.5 CenterZ=0 NormalX=0 NormalY=0 NormalZ=1 AngleXU=0 Radius=0.75
    g52: Circle CenterX=11.6913 CenterY=6.75 CenterZ=0 NormalX=0 NormalY=0 NormalZ=1 AngleXU=0 Radius=0.75
    g53: Circle CenterX=9.09327 CenterY=5.25 CenterZ=0 NormalX=0 NormalY=0 NormalZ=1 AngleXU=0 Radius=0.75
    g54: Circle CenterX=6.49519 CenterY=3.75 CenterZ=0 NormalX=0 NormalY=0 NormalZ=1 AngleXU=0 Radius=0.75
    g55: Circle CenterX=11.6913 CenterY=-6.75 CenterZ=0 NormalX=0 NormalY=0 NormalZ=1 AngleXU=0 Radius=0.75
    g56: Circle CenterX=9.09327 CenterY=-5.25 CenterZ=0 NormalX=0 NormalY=0 NormalZ=1 AngleXU=0 Radius=0.75
    g57: Circle CenterX=6.49519 CenterY=-3.75 CenterZ=0 NormalX=0 NormalY=0 NormalZ=1 AngleXU=0 Radius=0.75
    g58: Circle CenterX=9.8e-15 CenterY=-7.5 CenterZ=0 NormalX=0 NormalY=0 NormalZ=1 AngleXU=0 Radius=0.75
    g59: Circle CenterX=-1.42e-14 CenterY=-10.5 CenterZ=0 NormalX=0 NormalY=0 NormalZ=1 AngleXU=0 Radius=0.75
    g60: Circle CenterX=0 CenterY=-13.5 CenterZ=0 NormalX=0 NormalY=0 NormalZ=1 AngleXU=0 Radius=0.75
    g61: Circle CenterX=-11.6913 CenterY=-6.75 CenterZ=0 NormalX=0 NormalY=0 NormalZ=1 AngleXU=0 Radius=0.75
    g62: Circle CenterX=-9.09327 CenterY=-5.25 CenterZ=0 NormalX=0 NormalY=0 NormalZ=1 AngleXU=0 Radius=0.75
    g63: Circle CenterX=-6.49519 CenterY=-3.75 CenterZ=0 NormalX=0 NormalY=0 NormalZ=1 AngleXU=0 Radius=0.75
  constraints (136):
    c: Coincident(g0,g1)
    c: Coincident(g1,g2)
    c: Coincident(g2,g3)
    c: Coincident(g3,g4)
    c: Coincident(g4,g5)
    c: Coincident(g5,g0)
    c: Equal(g0, g1-g5) x5
    c: PointOnObject(g0,g6)
    c: PointOnObject(g1,g6)
    c: PointOnObject(g2,g6)
    c: PointOnObject(g3,g6)
    c: PointOnObject(g4,g6)
    c: PointOnObject(g5,g6)
    c: Coincident(g6,g-1)
    c: Coincident(g7,g8)
    c: Coincident(g8,g9)
    c: Coincident(g9,g10)
    c: Coincident(g10,g11)
    c: Coincident(g11,g12)
    c: Coincident(g12,g7)
    c: Equal(g7, g8-g12) x5
    c: PointOnObject(g7,g13)
    c: PointOnObject(g8,g13)
    c: PointOnObject(g9,g13)
    c: PointOnObject(g10,g13)
    c: PointOnObject(g11,g13)
    c: PointOnObject(g12,g13)
    c: Coincident(g13,g-1)
    c: PointOnObject(g12,g6)
    c: PointOnObject(g7,g-2)
    c: Horizontal(g5)
    c: Radius(g6) = 7.5
    c: Coincident(g14,g15)
    c: Coincident(g15,g16)
    c: Coincident(g16,g17)
    c: Coincident(g17,g18)
    c: Coincident(g18,g19)
    c: Coincident(g19,g14)
    c: Equal(g14, g15-g19) x5
    c: PointOnObject(g14,g20)
    c: PointOnObject(g15,g20)
    c: PointOnObject(g16,g20)
    c: PointOnObject(g17,g20)
    c: PointOnObject(g18,g20)
    c: PointOnObject(g19,g20)
    c: Coincident(g20,g-1)
    c: PointOnObject(g19,g-2)
    c: Radius(g20) = 10.5
    c: Coincident(g21,g22)
    c: Coincident(g22,g23)
    c: Coincident(g23,g24)
    c: Coincident(g24,g25)
    c: Coincident(g25,g26)
    c: Coincident(g26,g21)
    c: Equal(g21, g22-g26) x5
    c: PointOnObject(g21,g27)
    c: PointOnObject(g22,g27)
    c: PointOnObject(g23,g27)
    c: PointOnObject(g24,g27)
    c: PointOnObject(g25,g27)
    c: PointOnObject(g26,g27)
    c: Coincident(g27,g-1)
    c: PointOnObject(g26,g-2)
    c: Radius(g27) = 13.5
    c: Coincident(g28,g21)
    c: Coincident(g29,g25)
    c: Coincident(g30,g24)
    c: Coincident(g31,g23)
    c: Coincident(g32,g22)
    c: Coincident(g33,g21)
    c: Coincident(g34,g0)
    c: Coincident(g35,g34)
    c: Coincident(g36,g4)
    c: Coincident(g37,g36)
    c: Coincident(g38,g3)
    c: Coincident(g39,g38)
    c: Coincident(g40,g2)
    c: Coincident(g41,g40)
    c: Coincident(g42,g1)
    c: Coincident(g43,g42)
    c: Coincident(g44,g0)
    c: Coincident(g45,g44)
    c: Tangent(g35,g28) = 1.5708
    c: Tangent(g36,g28) = 1.5708
    c: Tangent(g37,g29) = 1.5708
    c: Tangent(g38,g29) = 1.5708
    c: Tangent(g39,g30) = 1.5708
    c: Tangent(g40,g30) = 1.5708
    c: Tangent(g41,g31) = 1.5708
    c: Tangent(g42,g31) = 1.5708
    c: Tangent(g43,g32) = 1.5708
    c: Tangent(g44,g32) = 1.5708
    c: Tangent(g45,g33) = 1.5708
    c: Tangent(g34,g33) = 1.5708
    c: Radius(g29) = 2.5
    c: Equal(g29,g28)
    c: Equal(g28,g33)
    c: Equal(g33,g32)
    c: Equal(g32,g31)
    c: Equal(g31,g30)
    c: Coincident(g46,g33)
    c: Coincident(g47,g14)
    c: Coincident(g48,g7)
    c: Coincident(g49,g28)
    c: Coincident(g50,g14)
    c: Coincident(g51,g7)
    c: Coincident(g52,g29)
    c: Coincident(g53,g18)
    c: Coincident(g54,g11)
    c: Coincident(g55,g30)
    c: Coincident(g56,g17)
    c: Coincident(g57,g10)
    c: Coincident(g58,g9)
    c: Coincident(g59,g16)
    c: Coincident(g60,g31)
    c: Coincident(g61,g32)
    c: Coincident(g62,g15)
    c: Coincident(g63,g8)
    c: Equal(g61,g62)
    c: Equal(g62,g63)
    c: Equal(g63,g58)
    c: Equal(g58,g59)
    c: Equal(g59,g60)
    c: Equal(g60,g55)
    c: Equal(g55,g56)
    c: Equal(g56,g57)
    c: Equal(g57,g54)
    c: Equal(g54,g53)
    c: Equal(g53,g52)
    c: Equal(g52,g51)
    c: Equal(g51,g50)
    c: Equal(g50,g49)
    c: Equal(g49,g46)
    c: Equal(g46,g47)
    c: Equal(g47,g48)
    c: Radius(g55) = 0.75
FEATURE [PartDesign::Pad] Pad993
  Length = 2
  Length2 = 100
  Profile = -> Sketch2351
  Type = 0
FEATURE [Sketcher::SketchObject] Sketch2349
  MapMode = 5
  Placement = pos=(0,0,2) rot=(0,0,1;0rad)
  Support = -> [Pad993]
  sketch-geometry (2):
    g0: Circle CenterX=0 CenterY=0 CenterZ=0 NormalX=0 NormalY=0 NormalZ=1 AngleXU=0 Radius=5
    g1: Circle CenterX=0 CenterY=0 CenterZ=0 NormalX=0 NormalY=0 NormalZ=1 AngleXU=0 Radius=3.5
  constraints (4):
    c: Coincident(g0,g-1)
    c: Coincident(g1,g0)
    c: Radius(g1) = 3.5
    c: Radius(g0) = 5
FEATURE [PartDesign::Pocket] Pocket795
  BaseFeature = -> Pad993
  Length = 1
  Length2 = 100
  Profile = -> Sketch2349
  Type = 0
FEATURE [Sketcher::SketchObject] Sketch2348
  MapMode = 5
  Placement = pos=(0,0,2) rot=(0,0,1;0rad)
  Support = -> [Pocket795]
  sketch-geometry (1):
    g0: Circle CenterX=0 CenterY=0 CenterZ=0 NormalX=0 NormalY=0 NormalZ=1 AngleXU=0 Radius=3
  constraints (2):
    c: Coincident(g0,g-1)
    c: Radius(g0) = 3
FEATURE [PartDesign::Pocket] Pocket802
  BaseFeature = -> Pocket795
  Length = 1
  Length2 = 100
  Profile = -> Sketch2348
  Type = 0
FEATURE [Sketcher::SketchObject] Sketch2350
  MapMode = 5
  Placement = pos=(0,0,1) rot=(0,0,1;0rad)
  Support = -> [Pocket802]
  sketch-geometry (1):
    g0: Circle CenterX=0 CenterY=0 CenterZ=0 NormalX=0 NormalY=0 NormalZ=1 AngleXU=0 Radius=1.5
  constraints (2):
    c: Coincident(g0,g-1)
    c: Radius(g0) = 1.5
FEATURE [PartDesign::Pocket] Pocket799
  BaseFeature = -> Pocket802
  Length = 5
  Length2 = 100
  Profile = -> Sketch2350
  Type = 0
FEATURE [Sketcher::SketchObject] Sketch2352
  MapMode = 5
  Placement = pos=(0,0,0) rot=(1,0,0;3.14159rad)
  Support = -> [Pocket799]
  sketch-geometry (2):
    g0: Circle CenterX=0 CenterY=0 CenterZ=0 NormalX=0 NormalY=0 NormalZ=1 AngleXU=0 Radius=4.5
    g1: Circle CenterX=0 CenterY=0 CenterZ=0 NormalX=0 NormalY=0 NormalZ=1 AngleXU=0 Radius=3
  constraints (4):
    c: Coincident(g0,g-1)
    c: Coincident(g1,g0)
    c: Radius(g0) = 4.5
    c: Radius(g1) = 3
FEATURE [PartDesign::Pad] Pad988
  BaseFeature = -> Pocket799
  Length = 3
  Length2 = 100
  Profile = -> Sketch2352
  Type = 0
FEATURE [PartDesign::Fillet] Fillet254
  Base = -> Pad988 [Face5,Edge96,Face4]
  BaseFeature = -> Pad988
  Radius = 0.2
FEATURE [PartDesign::Body] Body629  label="M2x093"
  Group = -> [Sketch2337,Pad1022,Sketch2275,Pad1027,Sketch2263,Pocket813,Chamfer497]
  Origin = -> Origin931
  Tip = -> Chamfer497
FEATURE [PartDesign::Body] Body630  label="M2x094"
  Group = -> [Sketch2338,Pad1024,Sketch2277,Pad1026,Sketch2278,Pocket809,Chamfer489]
  Origin = -> Origin930
  Tip = -> Chamfer489
FEATURE [PartDesign::Body] Body631  label="Futuba FSH6B012"
  Group = -> [Sketch2256,Pad1009,Sketch2259,Pocket807,Sketch2254,Pocket812,Sketch2260,Pocket808,Sketch2257,Pad1012,Fillet253]
  Origin = -> Origin916
  Tip = -> Fillet253
FEATURE [App::Part] Part260  label="Servohorn020"
  Group = -> [Body631]
  Origin = -> Origin917
  Placement = pos=(0,0,-67) rot=(0,0,1;0rad)
FEATURE [PartDesign::Body] Body632  label="M2x095"
  Group = -> [Sketch2332,Pad1010,Sketch2262,Pad1020,Sketch2271,Pocket815,Chamfer496]
  Origin = -> Origin914
  Tip = -> Chamfer496
FEATURE [PartDesign::Body] Body633  label="M2 Nut082"
  Group = -> [Sketch2274,Pad1019,Sketch2339,Groove209,Chamfer493,Sketch2334,Sketch2265]
  Origin = -> Origin908
  Placement = pos=(0,0,2.75) rot=(0,0,1;0rad)
  Tip = -> Chamfer493
FEATURE [App::Part] Part256  label="M087"
  Group = -> [Body630,Body633]
  Origin = -> Origin940
  Placement = pos=(-9.8e-15,-10.5,80) rot=(0,1,0;3.14159rad)
FEATURE [PartDesign::Body] Body634  label="M2 Nut083"
  Group = -> [Sketch2340,Pad1023,Sketch2267,Groove206,Chamfer490,Sketch2264,Sketch2331]
  Origin = -> Origin939
  Placement = pos=(0,0,2.75) rot=(0,0,1;0rad)
  Tip = -> Chamfer490
FEATURE [App::Part] Part255  label="M086"
  Group = -> [Body632,Body634]
  Origin = -> Origin915
  Placement = pos=(-9.1,-5.25,80) rot=(0,1,0;3.14159rad)
FEATURE [PartDesign::Body] Body635  label="M2 Nut084"
  Group = -> [Sketch2333,Pad1028,Sketch2270,Groove205,Chamfer487,Sketch2255,Sketch2269]
  Origin = -> Origin936
  Placement = pos=(0,0,2.75) rot=(0,0,1;0rad)
  Tip = -> Chamfer487
FEATURE [App::Part] Part258  label="M089"
  Group = -> [Body629,Body635]
  Origin = -> Origin925
  Placement = pos=(9.1,-5.25,80) rot=(0,1,0;3.14159rad)
FEATURE [PartDesign::Body] Body636  label="M2 Nut085"
  Group = -> [Sketch2280,Pad1017,Sketch2283,Groove208,Chamfer494,Sketch2282,Sketch2252]
  Origin = -> Origin929
  Placement = pos=(0,0,2.75) rot=(0,0,1;0rad)
  Tip = -> Chamfer494
FEATURE [PartDesign::Body] Body637  label="M2 Nut086"
  Group = -> [Sketch2335,Pad1025,Sketch2330,Groove210,Chamfer495,Sketch2318,Sketch2326]
  Origin = -> Origin935
  Placement = pos=(0,0,2.75) rot=(0,0,1;0rad)
  Tip = -> Chamfer495
FEATURE [PartDesign::Body] Body638  label="M2x096"
  Group = -> [Sketch2261,Pad1014,Sketch2258,Pad1013,Sketch2268,Pocket810,Chamfer486]
  Origin = -> Origin942
  Tip = -> Chamfer486
FEATURE [App::Part] Part259  label="M090"
  Group = -> [Body638,Body636]
  Origin = -> Origin918
  Placement = pos=(-9.1,5.25,80) rot=(0,1,0;3.14159rad)
FEATURE [PartDesign::Body] Body639  label="M2 Nut087"
  Group = -> [Sketch2266,Pad1015,Sketch2279,Groove207,Chamfer491,Sketch2281,Sketch2253]
  Origin = -> Origin937
  Placement = pos=(0,0,2.75) rot=(0,0,1;0rad)
  Tip = -> Chamfer491
FEATURE [PartDesign::Body] Body640  label="M2x097"
  Group = -> [Sketch2276,Pad1021,Sketch2273,Pad1016,Sketch2272,Pocket811,Chamfer488]
  Origin = -> Origin934
  Tip = -> Chamfer488
FEATURE [App::Part] Part257  label="M088"
  Group = -> [Body640,Body639]
  Origin = -> Origin938
  Placement = pos=(9.1,5.25,80) rot=(0,1,0;3.14159rad)
FEATURE [PartDesign::Body] Body641  label="Outer_Shoulder001"
  Group = -> [Sketch2341,Pad989,Sketch2346,Pocket798,Sketch2342,Pocket794,Sketch2344,Pocket796,Sketch2343,Pocket792,Sketch2347,Pocket797,Sketch2345,Pocket793,Fillet252]
  Origin = -> Origin911
  Placement = pos=(114.75,-99.65,166.6) rot=(0.57735,0.57735,0.57735;2.0944rad)
  Tip = -> Fillet252
FEATURE [PartDesign::Body] Body642  label="M2x098"
  Group = -> [Sketch2288,Pad990,Sketch2284,Pad996,Sketch2289,Pocket804,Chamfer483]
  Origin = -> Origin922
  Tip = -> Chamfer483
FEATURE [PartDesign::Body] Body643  label="Futuba FSH6B013"
  Group = -> [Sketch2351,Pad993,Sketch2349,Pocket795,Sketch2348,Pocket802,Sketch2350,Pocket799,Sketch2352,Pad988,Fillet254]
  Origin = -> Origin900
  Tip = -> Fillet254
FEATURE [App::Part] Part244  label="Servohorn019"
  Group = -> [Body643]
  Origin = -> Origin903
  Placement = pos=(0,0,-67) rot=(0,0,1;0rad)
FEATURE [PartDesign::Body] Body644  label="M2 Nut088"
  Group = -> [Sketch2291,Pad1002,Sketch2287,Groove202,Chamfer482,Sketch2286,Sketch2285]
  Origin = -> Origin928
  Placement = pos=(0,0,2.75) rot=(0,0,1;0rad)
  Tip = -> Chamfer482
FEATURE [App::Part] Part249  label="M081"
  Group = -> [Body642,Body644]
  Origin = -> Origin924
  Placement = pos=(-9.8e-15,10.5,80) rot=(0,1,0;3.14159rad)
FEATURE [PartDesign::Body] Body645  label="M2x099"
  Group = -> [Sketch2293,Pad1001,Sketch2308,Pad1003,Sketch2309,Pocket800,Chamfer485]
  Origin = -> Origin907
  Tip = -> Chamfer485
FEATURE [PartDesign::Body] Body646  label="M2x100"
  Group = -> [Sketch2294,Pad994,Sketch2303,Pad997,Sketch2310,Pocket805,Chamfer481]
  Origin = -> Origin898
  Tip = -> Chamfer481
FEATURE [PartDesign::Body] Body647  label="M2 Nut089"
  Group = -> [Sketch2311,Pad995,Sketch2297,Groove203,Chamfer476,Sketch2296,Sketch2300]
  Origin = -> Origin896
  Placement = pos=(0,0,2.75) rot=(0,0,1;0rad)
  Tip = -> Chamfer476
FEATURE [App::Part] Part250  label="M082"
  Group = -> [Body645,Body647]
  Origin = -> Origin920
  Placement = pos=(-9.8e-15,-10.5,80) rot=(0,1,0;3.14159rad)
FEATURE [PartDesign::Body] Body648  label="M2 Nut090"
  Group = -> [Sketch2290,Pad1000,Sketch2304,Groove200,Chamfer475,Sketch2302,Sketch2292]
  Origin = -> Origin912
  Placement = pos=(0,0,2.75) rot=(0,0,1;0rad)
  Tip = -> Chamfer475
FEATURE [App::Part] Part246  label="M080"
  Group = -> [Body646,Body648]
  Origin = -> Origin901
  Placement = pos=(-9.1,-5.25,80) rot=(0,1,0;3.14159rad)
FEATURE [PartDesign::Body] Body649  label="M2 Nut091"
  Group = -> [Sketch2295,Pad1005,Sketch2315,Groove199,Chamfer484,Sketch2329,Sketch2313]
  Origin = -> Origin910
  Placement = pos=(0,0,2.75) rot=(0,0,1;0rad)
  Tip = -> Chamfer484
FEATURE [PartDesign::Body] Body650  label="M2 Nut092"
  Group = -> [Sketch2314,Pad1011,Sketch2323,Groove204,Chamfer478,Sketch2320,Sketch2324]
  Origin = -> Origin905
  Placement = pos=(0,0,2.75) rot=(0,0,1;0rad)
  Tip = -> Chamfer478
FEATURE [PartDesign::Body] Body651  label="M2x101"
  Group = -> [Sketch2328,Pad992,Sketch2327,Pad991,Sketch2305,Pocket801,Chamfer480]
  Origin = -> Origin906
  Tip = -> Chamfer480
FEATURE [App::Part] Part254  label="M085"
  Group = -> [Body651,Body650]
  Origin = -> Origin897
  Placement = pos=(-9.1,5.25,80) rot=(0,1,0;3.14159rad)
FEATURE [PartDesign::Body] Body652  label="M2 Nut093"
  Group = -> [Sketch2301,Pad1006,Sketch2312,Groove201,Chamfer474,Sketch2316,Sketch2325]
  Origin = -> Origin923
  Placement = pos=(0,0,2.75) rot=(0,0,1;0rad)
  Tip = -> Chamfer474
FEATURE [PartDesign::Body] Body653  label="M2x102"
  Group = -> [Sketch2307,Pad998,Sketch2317,Pad1007,Sketch2321,Pocket806,Chamfer479]
  Origin = -> Origin927
  Tip = -> Chamfer479
FEATURE [App::Part] Part252  label="M083"
  Group = -> [Body653,Body652]
  Origin = -> Origin921
  Placement = pos=(9.1,5.25,80) rot=(0,1,0;3.14159rad)
FEATURE [PartDesign::Body] Body654  label="M2x103"
  Group = -> [Sketch2298,Pad999,Sketch2306,Pad1004,Sketch2299,Pocket803,Chamfer477]
  Origin = -> Origin913
  Tip = -> Chamfer477
FEATURE [App::Part] Part253  label="M084"
  Group = -> [Body654,Body649]
  Origin = -> Origin902
  Placement = pos=(9.1,-5.25,80) rot=(0,1,0;3.14159rad)
FEATURE [App::Part] Part248  label="Screws017"
  Group = -> [Part249,Part250,Part246,Part253,Part252,Part254]
  Origin = -> Origin904
  Placement = pos=(0,0,-141) rot=(0,0,1;0rad)
FEATURE [PartDesign::Body] Body655  label="M2x104"
  Group = -> [Sketch2319,Pad1008,Sketch2322,Pad1018,Sketch2336,Pocket814,Chamfer492]
  Origin = -> Origin941
  Tip = -> Chamfer492
FEATURE [App::Part] Part263  label="M091"
  Group = -> [Body655,Body637]
  Origin = -> Origin933
  Placement = pos=(-9.8e-15,10.5,80) rot=(0,1,0;3.14159rad)
FEATURE [App::Part] Part262  label="Screws018"
  Group = -> [Part263,Part256,Part255,Part258,Part257,Part259]
  Origin = -> Origin926
  Placement = pos=(0,0,-141) rot=(0,0,1;0rad)
FEATURE [Sketcher::SketchObject] Sketch2354
  MapMode = 5
  Support = -> [XY_Plane941]
  sketch-geometry (1):
    g0: Circle CenterX=0 CenterY=0 CenterZ=0 NormalX=0 NormalY=0 NormalZ=1 AngleXU=0 Radius=2.75
  constraints (2):
    c: Coincident(g0,g-1)
    c: Radius(g0) = 2.75
FEATURE [PartDesign::Pad] Pad987  label="M3x8 Head140"
  Length = 3
  Length2 = 100
  Profile = -> Sketch2354
  Type = 0
FEATURE [Sketcher::SketchObject] Sketch2356
  MapMode = 5
  Support = -> [XY_Plane942]
  sketch-geometry (1):
    g0: Circle CenterX=0 CenterY=0 CenterZ=0 NormalX=0 NormalY=0 NormalZ=1 AngleXU=0 Radius=2.75
  constraints (2):
    c: Coincident(g0,g-1)
    c: Radius(g0) = 2.75
FEATURE [PartDesign::Pad] Pad985  label="M3x8 Head139"
  Length = 3
  Length2 = 100
  Profile = -> Sketch2356
  Type = 0
FEATURE [Sketcher::SketchObject] Sketch2357
  MapMode = 5
  Placement = pos=(0,0,3) rot=(0,0,1;0rad)
  Support = -> [Pad985]
  sketch-geometry (1):
    g0: Circle CenterX=0 CenterY=0 CenterZ=0 NormalX=0 NormalY=0 NormalZ=1 AngleXU=0 Radius=1.5
  constraints (2):
    c: Coincident(g0,g-1)
    c: Radius(g0) = 1.5
FEATURE [PartDesign::Pad] Pad986  label="M3x8 Thread140"
  BaseFeature = -> Pad985
  Length = 8
  Length2 = 100
  Profile = -> Sketch2357
  Type = 0
FEATURE [Sketcher::SketchObject] Sketch2355
  MapMode = 5
  Placement = pos=(0,0,0) rot=(1,0,0;3.14159rad)
  Support = -> [Pad986]
  sketch-geometry (7):
    g0: LineSegment StartX=1.275 StartY=0.736122 StartZ=0 EndX=0 EndY=1.47224 EndZ=0
    g1: LineSegment StartX=0 StartY=1.47224 StartZ=0 EndX=-1.275 EndY=0.736122 EndZ=0
    g2: LineSegment StartX=-1.275 StartY=0.736122 StartZ=0 EndX=-1.275 EndY=-0.736122 EndZ=0
    g3: LineSegment StartX=-1.275 StartY=-0.736122 StartZ=0 EndX=1.34766e-11 EndY=-1.47224 EndZ=0
    g4: LineSegment StartX=1.34766e-11 StartY=-1.47224 StartZ=0 EndX=1.275 EndY=-0.736122 EndZ=0
    g5: LineSegment StartX=1.275 StartY=-0.736122 StartZ=0 EndX=1.275 EndY=0.736122 EndZ=0
    g6: Circle [constr] CenterX=0 CenterY=0 CenterZ=0 NormalX=0 NormalY=0 NormalZ=1 AngleXU=0 Radius=1.47224
  constraints (16):
    c: Coincident(g0,g1)
    c: Coincident(g1,g2)
    c: Coincident(g2,g3)
    c: Coincident(g3,g4)
    c: Coincident(g4,g5)
    c: Coincident(g5,g0)
    c: Equal(g0, g1-g5) x5
    c: PointOnObject(g0,g6)
    c: PointOnObject(g1,g6)
    c: PointOnObject(g2,g6)
    c: PointOnObject(g3,g6)
    c: PointOnObject(g4,g6)
    c: PointOnObject(g5,g6)
    c: Coincident(g6,g-1)
    c: PointOnObject(g0,g-2)
    c: DistanceX(g1,g0) = 2.55
FEATURE [PartDesign::Pocket] Pocket790  label="M3x8 Wrench139"
  BaseFeature = -> Pad986
  Length = 1.3
  Length2 = 100
  Profile = -> Sketch2355
  Type = 0
FEATURE [PartDesign::Chamfer] Chamfer498  label="M3x8 Smooth150"
  Base = -> Pocket790 [Face11,Edge2,Edge24,Edge3]
  BaseFeature = -> Pocket790
  Size = 0.2
FEATURE [PartDesign::Body] Body627  label="FOS Servohorn Left M3x009"
  Group = -> [Sketch2356,Pad985,Sketch2357,Pad986,Sketch2355,Pocket790,Chamfer498]
  Origin = -> Origin943
  Placement = pos=(8e-15,0,-63) rot=(0,1,0;3.14159rad)
  Tip = -> Chamfer498
FEATURE [App::Part] Part245  label="FOS Servohorn Left001"
  Group = -> [Part244,Part248,Body627]
  Origin = -> Origin919
  Placement = pos=(184.85,-60.65,210.6) rot=(-0.57735,-0.57735,-0.57735;4.18879rad)
FEATURE [Sketcher::SketchObject] Sketch2358
  MapMode = 5
  Placement = pos=(0,0,3) rot=(0,0,1;0rad)
  Support = -> [Pad987]
  sketch-geometry (1):
    g0: Circle CenterX=0 CenterY=0 CenterZ=0 NormalX=0 NormalY=0 NormalZ=1 AngleXU=0 Radius=1.5
  constraints (2):
    c: Coincident(g0,g-1)
    c: Radius(g0) = 1.5
FEATURE [PartDesign::Pad] Pad984  label="M3x8 Thread139"
  BaseFeature = -> Pad987
  Length = 8
  Length2 = 100
  Profile = -> Sketch2358
  Type = 0
FEATURE [Sketcher::SketchObject] Sketch2353
  MapMode = 5
  Placement = pos=(0,0,0) rot=(1,0,0;3.14159rad)
  Support = -> [Pad984]
  sketch-geometry (7):
    g0: LineSegment StartX=1.275 StartY=0.736122 StartZ=0 EndX=0 EndY=1.47224 EndZ=0
    g1: LineSegment StartX=0 StartY=1.47224 StartZ=0 EndX=-1.275 EndY=0.736122 EndZ=0
    g2: LineSegment StartX=-1.275 StartY=0.736122 StartZ=0 EndX=-1.275 EndY=-0.736122 EndZ=0
    g3: LineSegment StartX=-1.275 StartY=-0.736122 StartZ=0 EndX=1.34766e-11 EndY=-1.47224 EndZ=0
    g4: LineSegment StartX=1.34766e-11 StartY=-1.47224 StartZ=0 EndX=1.275 EndY=-0.736122 EndZ=0
    g5: LineSegment StartX=1.275 StartY=-0.736122 StartZ=0 EndX=1.275 EndY=0.736122 EndZ=0
    g6: Circle [constr] CenterX=0 CenterY=0 CenterZ=0 NormalX=0 NormalY=0 NormalZ=1 AngleXU=0 Radius=1.47224
  constraints (16):
    c: Coincident(g0,g1)
    c: Coincident(g1,g2)
    c: Coincident(g2,g3)
    c: Coincident(g3,g4)
    c: Coincident(g4,g5)
    c: Coincident(g5,g0)
    c: Equal(g0, g1-g5) x5
    c: PointOnObject(g0,g6)
    c: PointOnObject(g1,g6)
    c: PointOnObject(g2,g6)
    c: PointOnObject(g3,g6)
    c: PointOnObject(g4,g6)
    c: PointOnObject(g5,g6)
    c: Coincident(g6,g-1)
    c: PointOnObject(g0,g-2)
    c: DistanceX(g1,g0) = 2.55
FEATURE [PartDesign::Pocket] Pocket791  label="M3x8 Wrench140"
  BaseFeature = -> Pad984
  Length = 1.3
  Length2 = 100
  Profile = -> Sketch2353
  Type = 0
FEATURE [PartDesign::Chamfer] Chamfer499  label="M3x8 Smooth151"
  Base = -> Pocket791 [Face11,Edge2,Edge24,Edge3]
  BaseFeature = -> Pocket791
  Size = 0.2
FEATURE [PartDesign::Body] Body628  label="FOS Servohorn Right M3x009"
  Group = -> [Sketch2354,Pad987,Sketch2358,Pad984,Sketch2353,Pocket791,Chamfer499]
  Origin = -> Origin944
  Placement = pos=(0,0,-63) rot=(0,1,0;3.14159rad)
  Tip = -> Chamfer499
FEATURE [App::Part] Part261  label="FOS Servohorn Right001"
  Group = -> [Part260,Part262,Body628]
  Origin = -> Origin932
  Placement = pos=(184.9,-138.65,210.65) rot=(0.57735,0.57735,0.57735;2.0944rad)
FEATURE [App::Part] Part247  label="Front Outer Shoulder001"
  Group = -> [Body641,Part245,Part261]
  Origin = -> Origin909
FEATURE [App::Part] Part251  label="Rear Shoulder"
  Group = -> [Part247]
  Origin = -> Origin899
  Placement = pos=(-121,-199.5,0) rot=(0,0,1;3.14159rad)
FEATURE [Sketcher::SketchObject] Sketch022
  MapMode = 5
  Support = -> [XY_Plane963]
  sketch-geometry (8):
    g0: LineSegment StartX=0 StartY=3.17543 StartZ=0 EndX=-2.75 EndY=1.58771 EndZ=0
    g1: LineSegment StartX=-2.75 StartY=1.58771 StartZ=0 EndX=-2.75 EndY=-1.58771 EndZ=0
    g2: LineSegment StartX=-2.75 StartY=-1.58771 StartZ=0 EndX=0 EndY=-3.17543 EndZ=0
    g3: LineSegment StartX=0 StartY=-3.17543 StartZ=0 EndX=2.75 EndY=-1.58771 EndZ=0
    g4: LineSegment StartX=2.75 StartY=-1.58771 StartZ=0 EndX=2.75 EndY=1.58771 EndZ=0
    g5: LineSegment StartX=2.75 StartY=1.58771 StartZ=0 EndX=0 EndY=3.17543 EndZ=0
    g6: Circle [constr] CenterX=0 CenterY=0 CenterZ=0 NormalX=0 NormalY=0 NormalZ=1 AngleXU=0 Radius=3.17543
    g7: Circle CenterX=0 CenterY=0 CenterZ=0 NormalX=0 NormalY=0 NormalZ=1 AngleXU=0 Radius=1.5
  constraints (18):
    c: Coincident(g0,g1)
    c: Coincident(g1,g2)
    c: Coincident(g2,g3)
    c: Coincident(g3,g4)
    c: Coincident(g4,g5)
    c: Coincident(g5,g0)
    c: Equal(g0, g1-g5) x5
    c: PointOnObject(g0,g6)
    c: PointOnObject(g1,g6)
    c: PointOnObject(g2,g6)
    c: PointOnObject(g3,g6)
    c: PointOnObject(g4,g6)
    c: PointOnObject(g5,g6)
    c: Coincident(g6,g-1)
    c: PointOnObject(g5,g-2)
    c: DistanceX(g0,g4) = 5.5
    c: Coincident(g7,g-1)
    c: Radius(g7) = 1.5
FEATURE [Sketcher::SketchObject] Sketch060
  MapMode = 5
  Support = -> [XY_Plane956]
  sketch-geometry (4):
    g0: LineSegment StartX=-10 StartY=23.75 StartZ=0 EndX=10 EndY=23.75 EndZ=0
    g1: LineSegment StartX=10 StartY=23.75 StartZ=0 EndX=10 EndY=-23.75 EndZ=0
    g2: LineSegment StartX=10 StartY=-23.75 StartZ=0 EndX=-10 EndY=-23.75 EndZ=0
    g3: LineSegment StartX=-10 StartY=-23.75 StartZ=0 EndX=-10 EndY=23.75 EndZ=0
  constraints (10):
    c: Coincident(g0,g1)
    c: Coincident(g1,g2)
    c: Coincident(g2,g3)
    c: Coincident(g3,g0)
    c: Horizontal(g2)
    c: Vertical(g1)
    c: Symmetric(g0,g0,g-2)
    c: Symmetric(g0,g2,g-1)
    c: DistanceX(g0,g0) = 20
    c: DistanceY(g3,g3) = 47.5
FEATURE [Sketcher::SketchObject] Sketch020
  MapMode = 5
  Support = -> [XY_Plane948]
  sketch-geometry (8):
    g0: LineSegment StartX=0 StartY=3.17543 StartZ=0 EndX=-2.75 EndY=1.58771 EndZ=0
    g1: LineSegment StartX=-2.75 StartY=1.58771 StartZ=0 EndX=-2.75 EndY=-1.58771 EndZ=0
    g2: LineSegment StartX=-2.75 StartY=-1.58771 StartZ=0 EndX=0 EndY=-3.17543 EndZ=0
    g3: LineSegment StartX=0 StartY=-3.17543 StartZ=0 EndX=2.75 EndY=-1.58771 EndZ=0
    g4: LineSegment StartX=2.75 StartY=-1.58771 StartZ=0 EndX=2.75 EndY=1.58771 EndZ=0
    g5: LineSegment StartX=2.75 StartY=1.58771 StartZ=0 EndX=0 EndY=3.17543 EndZ=0
    g6: Circle [constr] CenterX=0 CenterY=0 CenterZ=0 NormalX=0 NormalY=0 NormalZ=1 AngleXU=0 Radius=3.17543
    g7: Circle CenterX=0 CenterY=0 CenterZ=0 NormalX=0 NormalY=0 NormalZ=1 AngleXU=0 Radius=1.5
  constraints (18):
    c: Coincident(g0,g1)
    c: Coincident(g1,g2)
    c: Coincident(g2,g3)
    c: Coincident(g3,g4)
    c: Coincident(g4,g5)
    c: Coincident(g5,g0)
    c: Equal(g0, g1-g5) x5
    c: PointOnObject(g0,g6)
    c: PointOnObject(g1,g6)
    c: PointOnObject(g2,g6)
    c: PointOnObject(g3,g6)
    c: PointOnObject(g4,g6)
    c: PointOnObject(g5,g6)
    c: Coincident(g6,g-1)
    c: PointOnObject(g5,g-2)
    c: DistanceX(g0,g4) = 5.5
    c: Coincident(g7,g-1)
    c: Radius(g7) = 1.5
FEATURE [Sketcher::SketchObject] Sketch067
  MapMode = 5
  Support = -> [XY_Plane964]
  sketch-geometry (8):
    g0: LineSegment StartX=0 StartY=3.17543 StartZ=0 EndX=-2.75 EndY=1.58771 EndZ=0
    g1: LineSegment StartX=-2.75 StartY=1.58771 StartZ=0 EndX=-2.75 EndY=-1.58771 EndZ=0
    g2: LineSegment StartX=-2.75 StartY=-1.58771 StartZ=0 EndX=0 EndY=-3.17543 EndZ=0
    g3: LineSegment StartX=0 StartY=-3.17543 StartZ=0 EndX=2.75 EndY=-1.58771 EndZ=0
    g4: LineSegment StartX=2.75 StartY=-1.58771 StartZ=0 EndX=2.75 EndY=1.58771 EndZ=0
    g5: LineSegment StartX=2.75 StartY=1.58771 StartZ=0 EndX=0 EndY=3.17543 EndZ=0
    g6: Circle [constr] CenterX=0 CenterY=0 CenterZ=0 NormalX=0 NormalY=0 NormalZ=1 AngleXU=0 Radius=3.17543
    g7: Circle CenterX=0 CenterY=0 CenterZ=0 NormalX=0 NormalY=0 NormalZ=1 AngleXU=0 Radius=1.5
  constraints (18):
    c: Coincident(g0,g1)
    c: Coincident(g1,g2)
    c: Coincident(g2,g3)
    c: Coincident(g3,g4)
    c: Coincident(g4,g5)
    c: Coincident(g5,g0)
    c: Equal(g0, g1-g5) x5
    c: PointOnObject(g0,g6)
    c: PointOnObject(g1,g6)
    c: PointOnObject(g2,g6)
    c: PointOnObject(g3,g6)
    c: PointOnObject(g4,g6)
    c: PointOnObject(g5,g6)
    c: Coincident(g6,g-1)
    c: PointOnObject(g5,g-2)
    c: DistanceX(g0,g4) = 5.5
    c: Coincident(g7,g-1)
    c: Radius(g7) = 1.5
FEATURE [Sketcher::SketchObject] Sketch066
  MapMode = 5
  Support = -> [XY_Plane962]
  sketch-geometry (8):
    g0: LineSegment StartX=0 StartY=3.17543 StartZ=0 EndX=-2.75 EndY=1.58771 EndZ=0
    g1: LineSegment StartX=-2.75 StartY=1.58771 StartZ=0 EndX=-2.75 EndY=-1.58771 EndZ=0
    g2: LineSegment StartX=-2.75 StartY=-1.58771 StartZ=0 EndX=0 EndY=-3.17543 EndZ=0
    g3: LineSegment StartX=0 StartY=-3.17543 StartZ=0 EndX=2.75 EndY=-1.58771 EndZ=0
    g4: LineSegment StartX=2.75 StartY=-1.58771 StartZ=0 EndX=2.75 EndY=1.58771 EndZ=0
    g5: LineSegment StartX=2.75 StartY=1.58771 StartZ=0 EndX=0 EndY=3.17543 EndZ=0
    g6: Circle [constr] CenterX=0 CenterY=0 CenterZ=0 NormalX=0 NormalY=0 NormalZ=1 AngleXU=0 Radius=3.17543
    g7: Circle CenterX=0 CenterY=0 CenterZ=0 NormalX=0 NormalY=0 NormalZ=1 AngleXU=0 Radius=1.5
  constraints (18):
    c: Coincident(g0,g1)
    c: Coincident(g1,g2)
    c: Coincident(g2,g3)
    c: Coincident(g3,g4)
    c: Coincident(g4,g5)
    c: Coincident(g5,g0)
    c: Equal(g0, g1-g5) x5
    c: PointOnObject(g0,g6)
    c: PointOnObject(g1,g6)
    c: PointOnObject(g2,g6)
    c: PointOnObject(g3,g6)
    c: PointOnObject(g4,g6)
    c: PointOnObject(g5,g6)
    c: Coincident(g6,g-1)
    c: PointOnObject(g5,g-2)
    c: DistanceX(g0,g4) = 5.5
    c: Coincident(g7,g-1)
    c: Radius(g7) = 1.5
FEATURE [Sketcher::SketchObject] Sketch070
  MapMode = 5
  Support = -> [XY_Plane952]
  sketch-geometry (8):
    g0: LineSegment StartX=0 StartY=3.17543 StartZ=0 EndX=-2.75 EndY=1.58771 EndZ=0
    g1: LineSegment StartX=-2.75 StartY=1.58771 StartZ=0 EndX=-2.75 EndY=-1.58771 EndZ=0
    g2: LineSegment StartX=-2.75 StartY=-1.58771 StartZ=0 EndX=0 EndY=-3.17543 EndZ=0
    g3: LineSegment StartX=0 StartY=-3.17543 StartZ=0 EndX=2.75 EndY=-1.58771 EndZ=0
    g4: LineSegment StartX=2.75 StartY=-1.58771 StartZ=0 EndX=2.75 EndY=1.58771 EndZ=0
    g5: LineSegment StartX=2.75 StartY=1.58771 StartZ=0 EndX=0 EndY=3.17543 EndZ=0
    g6: Circle [constr] CenterX=0 CenterY=0 CenterZ=0 NormalX=0 NormalY=0 NormalZ=1 AngleXU=0 Radius=3.17543
    g7: Circle CenterX=0 CenterY=0 CenterZ=0 NormalX=0 NormalY=0 NormalZ=1 AngleXU=0 Radius=1.5
  constraints (18):
    c: Coincident(g0,g1)
    c: Coincident(g1,g2)
    c: Coincident(g2,g3)
    c: Coincident(g3,g4)
    c: Coincident(g4,g5)
    c: Coincident(g5,g0)
    c: Equal(g0, g1-g5) x5
    c: PointOnObject(g0,g6)
    c: PointOnObject(g1,g6)
    c: PointOnObject(g2,g6)
    c: PointOnObject(g3,g6)
    c: PointOnObject(g4,g6)
    c: PointOnObject(g5,g6)
    c: Coincident(g6,g-1)
    c: PointOnObject(g5,g-2)
    c: DistanceX(g0,g4) = 5.5
    c: Coincident(g7,g-1)
    c: Radius(g7) = 1.5
FEATURE [Sketcher::SketchObject] Sketch037
  MapMode = 5
  Support = -> [XY_Plane950]
  sketch-geometry (1):
    g0: Circle CenterX=0 CenterY=0 CenterZ=0 NormalX=0 NormalY=0 NormalZ=1 AngleXU=0 Radius=2.75
  constraints (2):
    c: Coincident(g0,g-1)
    c: Radius(g0) = 2.75
FEATURE [Sketcher::SketchObject] Sketch039
  MapMode = 5
  Support = -> [XY_Plane961]
  sketch-geometry (1):
    g0: Circle CenterX=0 CenterY=0 CenterZ=0 NormalX=0 NormalY=0 NormalZ=1 AngleXU=0 Radius=2.75
  constraints (2):
    c: Coincident(g0,g-1)
    c: Radius(g0) = 2.75
FEATURE [Sketcher::SketchObject] Sketch042
  MapMode = 5
  Support = -> [XY_Plane026]
  sketch-geometry (1):
    g0: Circle CenterX=0 CenterY=0 CenterZ=0 NormalX=0 NormalY=0 NormalZ=1 AngleXU=0 Radius=2.75
  constraints (2):
    c: Coincident(g0,g-1)
    c: Radius(g0) = 2.75
FEATURE [Sketcher::SketchObject] Sketch044
  MapMode = 5
  Support = -> [XY_Plane960]
  sketch-geometry (1):
    g0: Circle CenterX=0 CenterY=0 CenterZ=0 NormalX=0 NormalY=0 NormalZ=1 AngleXU=0 Radius=2.75
  constraints (2):
    c: Coincident(g0,g-1)
    c: Radius(g0) = 2.75
FEATURE [Sketcher::SketchObject] Sketch048
  MapMode = 5
  Support = -> [XY_Plane957]
  sketch-geometry (8):
    g0: LineSegment StartX=-35 StartY=70 StartZ=0 EndX=35 EndY=70 EndZ=0
    g1: LineSegment StartX=55 StartY=50 StartZ=0 EndX=55 EndY=25 EndZ=0
    g2: LineSegment StartX=30 StartY=0 StartZ=0 EndX=-30 EndY=0 EndZ=0
    g3: LineSegment StartX=-55 StartY=25 StartZ=0 EndX=-55 EndY=50 EndZ=0
    g4: ArcOfCircle CenterX=-35 CenterY=50 CenterZ=0 NormalX=0 NormalY=0 NormalZ=1 AngleXU=0 Radius=20 StartAngle=1.5708 EndAngle=3.14159
    g5: ArcOfCircle CenterX=35 CenterY=50 CenterZ=0 NormalX=0 NormalY=0 NormalZ=1 AngleXU=0 Radius=20 StartAngle=0 EndAngle=1.5708
    g6: ArcOfCircle CenterX=30 CenterY=25 CenterZ=0 NormalX=0 NormalY=0 NormalZ=1 AngleXU=0 Radius=25 StartAngle=4.71239 EndAngle=6.28319
    g7: ArcOfCircle CenterX=-30 CenterY=25 CenterZ=0 NormalX=0 NormalY=0 NormalZ=1 AngleXU=0 Radius=25 StartAngle=3.14159 EndAngle=4.71239
  constraints (19):
    c: Horizontal(g0)
    c: Horizontal(g2)
    c: Vertical(g1)
    c: Vertical(g3)
    c: Tangent(g3,g4) = 1.5708
    c: Tangent(g0,g4) = 1.5708
    c: Tangent(g0,g5) = 1.5708
    c: Tangent(g1,g5) = 1.5708
    c: Tangent(g1,g6) = 1.5708
    c: Tangent(g2,g6) = 1.5708
    c: Tangent(g2,g7) = 1.5708
    c: Tangent(g3,g7) = 1.5708
    c: Equal(g4,g5)
    c: Equal(g7,g6)
    c: Symmetric(g2,g2,g-1)
    c: Radius(g4) = 20
    c: Radius(g7) = 25
    c: DistanceY(g2,g0) = 70
    c: DistanceX(g3,g1) = 110
FEATURE [Sketcher::SketchObject] Sketch052
  MapMode = 5
  Support = -> [XY_Plane945]
  sketch-geometry (4):
    g0: LineSegment StartX=-20 StartY=23.75 StartZ=0 EndX=20 EndY=23.75 EndZ=0
    g1: LineSegment StartX=20 StartY=23.75 StartZ=0 EndX=20 EndY=-23.75 EndZ=0
    g2: LineSegment StartX=20 StartY=-23.75 StartZ=0 EndX=-20 EndY=-23.75 EndZ=0
    g3: LineSegment StartX=-20 StartY=-23.75 StartZ=0 EndX=-20 EndY=23.75 EndZ=0
  constraints (10):
    c: Coincident(g0,g1)
    c: Coincident(g1,g2)
    c: Coincident(g2,g3)
    c: Coincident(g3,g0)
    c: Horizontal(g2)
    c: Vertical(g1)
    c: Symmetric(g0,g0,g-2)
    c: Symmetric(g0,g2,g-1)
    c: DistanceX(g0,g0) = 40
    c: DistanceY(g3,g3) = 47.5
FEATURE [PartDesign::Pad] Pad020  label="Baseplate040"
  Length = 5
  Length2 = 100
  Profile = -> Sketch048
  Type = 0
FEATURE [Sketcher::SketchObject] Sketch058
  MapMode = 5
  Placement = pos=(0,0,5) rot=(0,0,1;0rad)
  Support = -> [Pad020]
  sketch-geometry (8):
    g0: LineSegment StartX=-10 StartY=58 StartZ=0 EndX=10 EndY=58 EndZ=0
    g1: LineSegment StartX=20 StartY=48 StartZ=0 EndX=20 EndY=22 EndZ=0
    g2: LineSegment StartX=10 StartY=12 StartZ=0 EndX=-10 EndY=12 EndZ=0
    g3: LineSegment StartX=-20 StartY=22 StartZ=0 EndX=-20 EndY=48 EndZ=0
    g4: ArcOfCircle CenterX=-10 CenterY=48 CenterZ=0 NormalX=0 NormalY=0 NormalZ=1 AngleXU=0 Radius=10 StartAngle=1.5708 EndAngle=3.14159
    g5: ArcOfCircle CenterX=10 CenterY=48 CenterZ=0 NormalX=0 NormalY=0 NormalZ=1 AngleXU=0 Radius=10 StartAngle=2e-16 EndAngle=1.5708
    g6: ArcOfCircle CenterX=10 CenterY=22 CenterZ=0 NormalX=0 NormalY=0 NormalZ=1 AngleXU=0 Radius=10 StartAngle=4.71239 EndAngle=6.28319
    g7: ArcOfCircle CenterX=-10 CenterY=22 CenterZ=0 NormalX=0 NormalY=0 NormalZ=1 AngleXU=0 Radius=10 StartAngle=3.14159 EndAngle=4.71239
  constraints (19):
    c: Horizontal(g0)
    c: Vertical(g1)
    c: Vertical(g3)
    c: Tangent(g3,g4) = 1.5708
    c: Tangent(g0,g4) = 1.5708
    c: Tangent(g0,g5) = 1.5708
    c: Tangent(g1,g5) = 1.5708
    c: Tangent(g1,g6) = 1.5708
    c: Tangent(g2,g6) = 1.5708
    c: Tangent(g2,g7) = 1.5708
    c: Tangent(g3,g7) = 1.5708
    c: Equal(g5,g4)
    c: Equal(g4,g7)
    c: Equal(g7,g6)
    c: Symmetric(g2,g2,g-2)
    c: DistanceX(g3,g1) = 40
    c: DistanceY(g-1,g2) = 12
    c: DistanceY(g2,g0) = 46
    c: Radius(g5) = 10
FEATURE [PartDesign::Pocket] Pocket022  label="Accesshole006"
  BaseFeature = -> Pad020
  Length = 5
  Length2 = 100
  Profile = -> Sketch058
  Type = 0
FEATURE [Sketcher::SketchObject] Sketch049
  MapMode = 5
  Placement = pos=(0,0,5) rot=(0,0,1;0rad)
  Support = -> [Pocket022]
  sketch-geometry (8):
    g0: Circle CenterX=-51.75 CenterY=45 CenterZ=0 NormalX=0 NormalY=0 NormalZ=1 AngleXU=0 Radius=1.6
    g1: Circle CenterX=-51.75 CenterY=30 CenterZ=0 NormalX=0 NormalY=0 NormalZ=1 AngleXU=0 Radius=1.6
    g2: Circle CenterX=-5 CenterY=6 CenterZ=0 NormalX=0 NormalY=0 NormalZ=1 AngleXU=0 Radius=1.6
    g3: Circle CenterX=5 CenterY=6 CenterZ=0 NormalX=0 NormalY=0 NormalZ=1 AngleXU=0 Radius=1.6
    g4: Circle CenterX=15 CenterY=64 CenterZ=0 NormalX=0 NormalY=0 NormalZ=1 AngleXU=0 Radius=1.6
    g5: Circle CenterX=-15 CenterY=64 CenterZ=0 NormalX=0 NormalY=0 NormalZ=1 AngleXU=0 Radius=1.6
    g6: Circle CenterX=51.75 CenterY=45 CenterZ=0 NormalX=0 NormalY=0 NormalZ=1 AngleXU=0 Radius=1.6
    g7: Circle CenterX=51.75 CenterY=30 CenterZ=0 NormalX=0 NormalY=0 NormalZ=1 AngleXU=0 Radius=1.6
  constraints (20):
    c: Equal(g1,g0)
    c: Equal(g1,g5)
    c: Equal(g1,g4)
    c: Equal(g1,g6)
    c: Equal(g1,g7)
    c: Equal(g1,g3)
    c: Equal(g1,g2)
    c: Symmetric(g2,g3,g-2)
    c: Symmetric(g5,g4,g-2)
    c: Symmetric(g0,g6,g-2)
    c: Symmetric(g1,g7,g-2)
    c: Vertical(g7,g6)
    c: DistanceX(g5,g4) = 30
    c: DistanceX(g2,g3) = 10
    c: DistanceY(g-1,g1) = 30
    c: DistanceY(g1,g0) = 15
    c: DistanceX(g1,g-1) = 51.75
    c: DistanceY(g-1,g2) = 6
    c: Radius(g6) = 1.6
    c: DistanceY(g-1,g4) = 64
FEATURE [PartDesign::Pad] Pad017  label="M3x8 Head001"
  Length = 3
  Length2 = 100
  Profile = -> Sketch044
  Type = 0
FEATURE [Sketcher::SketchObject] Sketch046
  MapMode = 5
  Placement = pos=(0,0,3) rot=(0,0,1;0rad)
  Support = -> [Pad017]
  sketch-geometry (1):
    g0: Circle CenterX=0 CenterY=0 CenterZ=0 NormalX=0 NormalY=0 NormalZ=1 AngleXU=0 Radius=1.5
  constraints (2):
    c: Coincident(g0,g-1)
    c: Radius(g0) = 1.5
FEATURE [PartDesign::Pad] Pad012  label="M3x8 Thread001"
  BaseFeature = -> Pad017
  Length = 8
  Length2 = 100
  Profile = -> Sketch046
  Type = 0
FEATURE [Sketcher::SketchObject] Sketch040
  MapMode = 5
  Placement = pos=(0,0,0) rot=(1,0,0;3.14159rad)
  Support = -> [Pad012]
  sketch-geometry (7):
    g0: LineSegment StartX=1.275 StartY=0.736122 StartZ=0 EndX=0 EndY=1.47224 EndZ=0
    g1: LineSegment StartX=0 StartY=1.47224 StartZ=0 EndX=-1.275 EndY=0.736122 EndZ=0
    g2: LineSegment StartX=-1.275 StartY=0.736122 StartZ=0 EndX=-1.275 EndY=-0.736122 EndZ=0
    g3: LineSegment StartX=-1.275 StartY=-0.736122 StartZ=0 EndX=1.34766e-11 EndY=-1.47224 EndZ=0
    g4: LineSegment StartX=1.34766e-11 StartY=-1.47224 StartZ=0 EndX=1.275 EndY=-0.736122 EndZ=0
    g5: LineSegment StartX=1.275 StartY=-0.736122 StartZ=0 EndX=1.275 EndY=0.736122 EndZ=0
    g6: Circle [constr] CenterX=0 CenterY=0 CenterZ=0 NormalX=0 NormalY=0 NormalZ=1 AngleXU=0 Radius=1.47224
  constraints (16):
    c: Coincident(g0,g1)
    c: Coincident(g1,g2)
    c: Coincident(g2,g3)
    c: Coincident(g3,g4)
    c: Coincident(g4,g5)
    c: Coincident(g5,g0)
    c: Equal(g0, g1-g5) x5
    c: PointOnObject(g0,g6)
    c: PointOnObject(g1,g6)
    c: PointOnObject(g2,g6)
    c: PointOnObject(g3,g6)
    c: PointOnObject(g4,g6)
    c: PointOnObject(g5,g6)
    c: Coincident(g6,g-1)
    c: PointOnObject(g0,g-2)
    c: DistanceX(g1,g0) = 2.55
FEATURE [PartDesign::Pocket] Pocket018  label="M3x8 Wrench001"
  BaseFeature = -> Pad012
  Length = 1.3
  Length2 = 100
  Profile = -> Sketch040
  Type = 0
FEATURE [PartDesign::Pad] Pad014  label="M3x8 Head002"
  Length = 3
  Length2 = 100
  Profile = -> Sketch037
  Type = 0
FEATURE [Sketcher::SketchObject] Sketch043
  MapMode = 5
  Placement = pos=(0,0,3) rot=(0,0,1;0rad)
  Support = -> [Pad014]
  sketch-geometry (1):
    g0: Circle CenterX=0 CenterY=0 CenterZ=0 NormalX=0 NormalY=0 NormalZ=1 AngleXU=0 Radius=1.5
  constraints (2):
    c: Coincident(g0,g-1)
    c: Radius(g0) = 1.5
FEATURE [PartDesign::Pad] Pad015  label="M3x8 Head153"
  Length = 3
  Length2 = 100
  Profile = -> Sketch039
  Type = 0
FEATURE [Sketcher::SketchObject] Sketch036
  MapMode = 5
  Placement = pos=(0,0,3) rot=(0,0,1;0rad)
  Support = -> [Pad015]
  sketch-geometry (1):
    g0: Circle CenterX=0 CenterY=0 CenterZ=0 NormalX=0 NormalY=0 NormalZ=1 AngleXU=0 Radius=1.5
  constraints (2):
    c: Coincident(g0,g-1)
    c: Radius(g0) = 1.5
FEATURE [PartDesign::Pad] Pad019  label="M3x8 Thread002"
  BaseFeature = -> Pad014
  Length = 8
  Length2 = 100
  Profile = -> Sketch043
  Type = 0
FEATURE [Sketcher::SketchObject] Sketch041
  MapMode = 5
  Placement = pos=(0,0,0) rot=(1,0,0;3.14159rad)
  Support = -> [Pad019]
  sketch-geometry (7):
    g0: LineSegment StartX=1.275 StartY=0.736122 StartZ=0 EndX=0 EndY=1.47224 EndZ=0
    g1: LineSegment StartX=0 StartY=1.47224 StartZ=0 EndX=-1.275 EndY=0.736122 EndZ=0
    g2: LineSegment StartX=-1.275 StartY=0.736122 StartZ=0 EndX=-1.275 EndY=-0.736122 EndZ=0
    g3: LineSegment StartX=-1.275 StartY=-0.736122 StartZ=0 EndX=1.34766e-11 EndY=-1.47224 EndZ=0
    g4: LineSegment StartX=1.34766e-11 StartY=-1.47224 StartZ=0 EndX=1.275 EndY=-0.736122 EndZ=0
    g5: LineSegment StartX=1.275 StartY=-0.736122 StartZ=0 EndX=1.275 EndY=0.736122 EndZ=0
    g6: Circle [constr] CenterX=0 CenterY=0 CenterZ=0 NormalX=0 NormalY=0 NormalZ=1 AngleXU=0 Radius=1.47224
  constraints (16):
    c: Coincident(g0,g1)
    c: Coincident(g1,g2)
    c: Coincident(g2,g3)
    c: Coincident(g3,g4)
    c: Coincident(g4,g5)
    c: Coincident(g5,g0)
    c: Equal(g0, g1-g5) x5
    c: PointOnObject(g0,g6)
    c: PointOnObject(g1,g6)
    c: PointOnObject(g2,g6)
    c: PointOnObject(g3,g6)
    c: PointOnObject(g4,g6)
    c: PointOnObject(g5,g6)
    c: Coincident(g6,g-1)
    c: PointOnObject(g0,g-2)
    c: DistanceX(g1,g0) = 2.55
FEATURE [PartDesign::Pocket] Pocket019  label="M3x8 Wrench002"
  BaseFeature = -> Pad019
  Length = 1.3
  Length2 = 100
  Profile = -> Sketch041
  Type = 0
FEATURE [PartDesign::Pad] Pad013  label="M3x8 Thread153"
  BaseFeature = -> Pad015
  Length = 8
  Length2 = 100
  Profile = -> Sketch036
  Type = 0
FEATURE [Sketcher::SketchObject] Sketch045
  MapMode = 5
  Placement = pos=(0,0,0) rot=(1,0,0;3.14159rad)
  Support = -> [Pad013]
  sketch-geometry (7):
    g0: LineSegment StartX=1.275 StartY=0.736122 StartZ=0 EndX=0 EndY=1.47224 EndZ=0
    g1: LineSegment StartX=0 StartY=1.47224 StartZ=0 EndX=-1.275 EndY=0.736122 EndZ=0
    g2: LineSegment StartX=-1.275 StartY=0.736122 StartZ=0 EndX=-1.275 EndY=-0.736122 EndZ=0
    g3: LineSegment StartX=-1.275 StartY=-0.736122 StartZ=0 EndX=1.34766e-11 EndY=-1.47224 EndZ=0
    g4: LineSegment StartX=1.34766e-11 StartY=-1.47224 StartZ=0 EndX=1.275 EndY=-0.736122 EndZ=0
    g5: LineSegment StartX=1.275 StartY=-0.736122 StartZ=0 EndX=1.275 EndY=0.736122 EndZ=0
    g6: Circle [constr] CenterX=0 CenterY=0 CenterZ=0 NormalX=0 NormalY=0 NormalZ=1 AngleXU=0 Radius=1.47224
  constraints (16):
    c: Coincident(g0,g1)
    c: Coincident(g1,g2)
    c: Coincident(g2,g3)
    c: Coincident(g3,g4)
    c: Coincident(g4,g5)
    c: Coincident(g5,g0)
    c: Equal(g0, g1-g5) x5
    c: PointOnObject(g0,g6)
    c: PointOnObject(g1,g6)
    c: PointOnObject(g2,g6)
    c: PointOnObject(g3,g6)
    c: PointOnObject(g4,g6)
    c: PointOnObject(g5,g6)
    c: Coincident(g6,g-1)
    c: PointOnObject(g0,g-2)
    c: DistanceX(g1,g0) = 2.55
FEATURE [PartDesign::Pocket] Pocket017  label="M3x8 Wrench153"
  BaseFeature = -> Pad013
  Length = 1.3
  Length2 = 100
  Profile = -> Sketch045
  Type = 0
FEATURE [PartDesign::Pad] Pad016  label="M3x8 Head003"
  Length = 3
  Length2 = 100
  Profile = -> Sketch042
  Type = 0
FEATURE [Sketcher::SketchObject] Sketch047
  MapMode = 5
  Placement = pos=(0,0,3) rot=(0,0,1;0rad)
  Support = -> [Pad016]
  sketch-geometry (1):
    g0: Circle CenterX=0 CenterY=0 CenterZ=0 NormalX=0 NormalY=0 NormalZ=1 AngleXU=0 Radius=1.5
  constraints (2):
    c: Coincident(g0,g-1)
    c: Radius(g0) = 1.5
FEATURE [PartDesign::Pad] Pad018  label="M3x8 Thread003"
  BaseFeature = -> Pad016
  Length = 8
  Length2 = 100
  Profile = -> Sketch047
  Type = 0
FEATURE [Sketcher::SketchObject] Sketch038
  MapMode = 5
  Placement = pos=(0,0,0) rot=(1,0,0;3.14159rad)
  Support = -> [Pad018]
  sketch-geometry (7):
    g0: LineSegment StartX=1.275 StartY=0.736122 StartZ=0 EndX=0 EndY=1.47224 EndZ=0
    g1: LineSegment StartX=0 StartY=1.47224 StartZ=0 EndX=-1.275 EndY=0.736122 EndZ=0
    g2: LineSegment StartX=-1.275 StartY=0.736122 StartZ=0 EndX=-1.275 EndY=-0.736122 EndZ=0
    g3: LineSegment StartX=-1.275 StartY=-0.736122 StartZ=0 EndX=1.34766e-11 EndY=-1.47224 EndZ=0
    g4: LineSegment StartX=1.34766e-11 StartY=-1.47224 StartZ=0 EndX=1.275 EndY=-0.736122 EndZ=0
    g5: LineSegment StartX=1.275 StartY=-0.736122 StartZ=0 EndX=1.275 EndY=0.736122 EndZ=0
    g6: Circle [constr] CenterX=0 CenterY=0 CenterZ=0 NormalX=0 NormalY=0 NormalZ=1 AngleXU=0 Radius=1.47224
  constraints (16):
    c: Coincident(g0,g1)
    c: Coincident(g1,g2)
    c: Coincident(g2,g3)
    c: Coincident(g3,g4)
    c: Coincident(g4,g5)
    c: Coincident(g5,g0)
    c: Equal(g0, g1-g5) x5
    c: PointOnObject(g0,g6)
    c: PointOnObject(g1,g6)
    c: PointOnObject(g2,g6)
    c: PointOnObject(g3,g6)
    c: PointOnObject(g4,g6)
    c: PointOnObject(g5,g6)
    c: Coincident(g6,g-1)
    c: PointOnObject(g0,g-2)
    c: DistanceX(g1,g0) = 2.55
FEATURE [PartDesign::Pocket] Pocket020  label="M3x8 Wrench003"
  BaseFeature = -> Pad018
  Length = 1.3
  Length2 = 100
  Profile = -> Sketch038
  Type = 0
FEATURE [PartDesign::Pocket] Pocket024  label="Screwholes010"
  BaseFeature = -> Pocket022
  Length = 5
  Length2 = 100
  Profile = -> Sketch049
  Type = 0
FEATURE [Sketcher::SketchObject] Sketch057
  ExternalGeometry = -> [Pocket024]
  MapMode = 5
  Placement = pos=(0,0,5) rot=(0,0,1;0rad)
  Support = -> [Pocket024]
  sketch-geometry (16):
    g0: ArcOfCircle CenterX=51.75 CenterY=45 CenterZ=0 NormalX=0 NormalY=0 NormalZ=1 AngleXU=0 Radius=3 StartAngle=1.5708 EndAngle=4.71239
    g1: ArcOfCircle CenterX=61.75 CenterY=45 CenterZ=0 NormalX=0 NormalY=0 NormalZ=1 AngleXU=0 Radius=3 StartAngle=4.71239 EndAngle=7.85398
    g2: LineSegment StartX=51.75 StartY=42 StartZ=0 EndX=61.75 EndY=42 EndZ=0
    g3: LineSegment StartX=51.75 StartY=48 StartZ=0 EndX=61.75 EndY=48 EndZ=0
    g4: ArcOfCircle CenterX=51.75 CenterY=30 CenterZ=0 NormalX=0 NormalY=0 NormalZ=1 AngleXU=0 Radius=3 StartAngle=1.5708 EndAngle=4.71239
    g5: ArcOfCircle CenterX=61.75 CenterY=30 CenterZ=0 NormalX=0 NormalY=0 NormalZ=1 AngleXU=0 Radius=3 StartAngle=4.71239 EndAngle=7.85398
    g6: LineSegment StartX=51.75 StartY=27 StartZ=0 EndX=61.75 EndY=27 EndZ=0
    g7: LineSegment StartX=51.75 StartY=33 StartZ=0 EndX=61.75 EndY=33 EndZ=0
    g8: ArcOfCircle CenterX=-51.75 CenterY=45 CenterZ=0 NormalX=0 NormalY=0 NormalZ=1 AngleXU=0 Radius=3 StartAngle=4.71239 EndAngle=7.85398
    g9: ArcOfCircle CenterX=-61.75 CenterY=45 CenterZ=0 NormalX=0 NormalY=0 NormalZ=1 AngleXU=0 Radius=3 StartAngle=1.5708 EndAngle=4.71239
    g10: LineSegment StartX=-51.75 StartY=48 StartZ=0 EndX=-61.75 EndY=48 EndZ=0
    g11: LineSegment StartX=-51.75 StartY=42 StartZ=0 EndX=-61.75 EndY=42 EndZ=0
    g12: ArcOfCircle CenterX=-51.75 CenterY=30 CenterZ=0 NormalX=0 NormalY=0 NormalZ=1 AngleXU=0 Radius=3 StartAngle=4.71239 EndAngle=7.85398
    g13: ArcOfCircle CenterX=-61.75 CenterY=30 CenterZ=0 NormalX=0 NormalY=0 NormalZ=1 AngleXU=0 Radius=3 StartAngle=1.5708 EndAngle=4.71239
    g14: LineSegment StartX=-51.75 StartY=33 StartZ=0 EndX=-61.75 EndY=33 EndZ=0
    g15: LineSegment StartX=-51.75 StartY=27 StartZ=0 EndX=-61.75 EndY=27 EndZ=0
  constraints (36):
    c: Tangent(g0,g3) = 1.5708
    c: Tangent(g0,g2) = -1.5708
    c: Tangent(g2,g1) = -1.5708
    c: Tangent(g3,g1) = 1.5708
    c: Horizontal(g2)
    c: Equal(g0,g1)
    c: Coincident(g0,g-5)
    c: Tangent(g4,g7) = 1.5708
    c: Tangent(g4,g6) = -1.5708
    c: Tangent(g6,g5) = -1.5708
    c: Tangent(g7,g5) = 1.5708
    c: Horizontal(g6)
    c: Equal(g4,g5)
    c: Coincident(g4,g-6)
    c: Tangent(g8,g11) = 1.5708
    c: Tangent(g8,g10) = -1.5708
    c: Tangent(g10,g9) = -1.5708
    c: Tangent(g11,g9) = 1.5708
    c: Horizontal(g10)
    c: Equal(g8,g9)
    c: Coincident(g8,g-3)
    c: Tangent(g12,g15) = 1.5708
    c: Tangent(g12,g14) = -1.5708
    c: Tangent(g14,g13) = -1.5708
    c: Tangent(g15,g13) = 1.5708
    c: Horizontal(g14)
    c: Equal(g12,g13)
    c: Coincident(g12,g-4)
    c: Equal(g8,g12)
    c: Equal(g12,g0)
    c: Equal(g0,g4)
    c: Equal(g3,g10)
    c: Equal(g10,g14)
    c: Equal(g14,g7)
    c: Radius(g1) = 3
    c: DistanceX(g3,g3) = 10
FEATURE [PartDesign::Pocket] Pocket023  label="Screwheads Top"
  BaseFeature = -> Pocket024
  Length = 3
  Length2 = 100
  Profile = -> Sketch057
  Type = 0
FEATURE [PartDesign::Pad] Pad1029  label="M3 Nut Primitive203"
  Length = 1.2
  Length2 = 1.2
  Profile = -> Sketch066
  Type = 4
FEATURE [Sketcher::SketchObject] Sketch063
  ExternalGeometry = -> [Pad1029]
  MapMode = 5
  Placement = pos=(0,0,0) rot=(0.57735,0.57735,0.57735;2.0944rad)
  Support = -> [YZ_Plane955]
  sketch-geometry (6):
    g0: LineSegment StartX=-2.67543 StartY=1.2 StartZ=0 EndX=-3.67543 EndY=1.2 EndZ=0
    g1: LineSegment StartX=-3.67543 StartY=1.2 StartZ=0 EndX=-3.67543 EndY=-1.2 EndZ=0
    g2: LineSegment StartX=-3.67543 StartY=-1.2 StartZ=0 EndX=-2.67543 EndY=-1.2 EndZ=0
    g3: LineSegment StartX=-2.67543 StartY=-1.2 StartZ=0 EndX=-3.17543 EndY=-1 EndZ=0
    g4: LineSegment StartX=-3.17543 StartY=-1 StartZ=0 EndX=-3.17543 EndY=1 EndZ=0
    g5: LineSegment StartX=-3.17543 StartY=1 StartZ=0 EndX=-2.67543 EndY=1.2 EndZ=0
  constraints (15):
    c: Horizontal(g0)
    c: Coincident(g0,g1)
    c: Coincident(g1,g2)
    c: Coincident(g2,g3)
    c: Coincident(g3,g4)
    c: Coincident(g4,g5)
    c: Coincident(g5,g0)
    c: Symmetric(g4,g3,g-1)
    c: Symmetric(g0,g2,g-1)
    c: Symmetric(g1,g0,g-1)
    c: DistanceX(g0,g4) = 0.5
    c: DistanceY(g3,g4) = 2
    c: DistanceY(g1,g0) = 2.4
    c: PointOnObject(g3,g-3)
    c: DistanceX(g4,g0) = 0.5
FEATURE [PartDesign::Groove] Groove211  label="M3 Nut Smooth203"
  Angle = 360
  Axis = (-2e-16,3e-16,1)
  Base = (0,0,0)
  BaseFeature = -> Pad1029
  Profile = -> Sketch063
  ReferenceAxis = -> Sketch063 [V_Axis]
  Reversed = true
FEATURE [PartDesign::Pad] Pad1030  label="Baseplate041"
  Length = 12
  Length2 = 100
  Profile = -> Sketch052
  Type = 0
FEATURE [Sketcher::SketchObject] Sketch2361
  MapMode = 5
  Placement = pos=(0,-23.75,0) rot=(1,0,0;1.5708rad)
  Support = -> [Pad1030]
  sketch-geometry (2):
    g0: Circle CenterX=-15 CenterY=6 CenterZ=0 NormalX=0 NormalY=0 NormalZ=1 AngleXU=0 Radius=1.6
    g1: Circle CenterX=15 CenterY=6 CenterZ=0 NormalX=0 NormalY=0 NormalZ=1 AngleXU=0 Radius=1.6
  constraints (5):
    c: Symmetric(g0,g1,g-2)
    c: Equal(g0,g1)
    c: Radius(g1) = 1.6
    c: DistanceY(g-1,g0) = 6
    c: DistanceX(g0,g1) = 30
FEATURE [PartDesign::Pad] Pad006  label="M3 Nut Primitive204"
  Length = 1.2
  Length2 = 1.2
  Profile = -> Sketch067
  Type = 4
FEATURE [Sketcher::SketchObject] Sketch068
  ExternalGeometry = -> [Pad006]
  MapMode = 5
  Placement = pos=(0,0,0) rot=(0.57735,0.57735,0.57735;2.0944rad)
  Support = -> [YZ_Plane958]
  sketch-geometry (6):
    g0: LineSegment StartX=-2.67543 StartY=1.2 StartZ=0 EndX=-3.67543 EndY=1.2 EndZ=0
    g1: LineSegment StartX=-3.67543 StartY=1.2 StartZ=0 EndX=-3.67543 EndY=-1.2 EndZ=0
    g2: LineSegment StartX=-3.67543 StartY=-1.2 StartZ=0 EndX=-2.67543 EndY=-1.2 EndZ=0
    g3: LineSegment StartX=-2.67543 StartY=-1.2 StartZ=0 EndX=-3.17543 EndY=-1 EndZ=0
    g4: LineSegment StartX=-3.17543 StartY=-1 StartZ=0 EndX=-3.17543 EndY=1 EndZ=0
    g5: LineSegment StartX=-3.17543 StartY=1 StartZ=0 EndX=-2.67543 EndY=1.2 EndZ=0
  constraints (15):
    c: Horizontal(g0)
    c: Coincident(g0,g1)
    c: Coincident(g1,g2)
    c: Coincident(g2,g3)
    c: Coincident(g3,g4)
    c: Coincident(g4,g5)
    c: Coincident(g5,g0)
    c: Symmetric(g4,g3,g-1)
    c: Symmetric(g0,g2,g-1)
    c: Symmetric(g1,g0,g-1)
    c: DistanceX(g0,g4) = 0.5
    c: DistanceY(g3,g4) = 2
    c: DistanceY(g1,g0) = 2.4
    c: PointOnObject(g3,g-3)
    c: DistanceX(g4,g0) = 0.5
FEATURE [PartDesign::Pad] Pad1031  label="M3 Nut Primitive205"
  Length = 1.2
  Length2 = 1.2
  Profile = -> Sketch020
  Type = 4
FEATURE [Sketcher::SketchObject] Sketch021
  ExternalGeometry = -> [Pad1031]
  MapMode = 5
  Placement = pos=(0,0,0) rot=(0.57735,0.57735,0.57735;2.0944rad)
  Support = -> [YZ_Plane939]
  sketch-geometry (6):
    g0: LineSegment StartX=-2.67543 StartY=1.2 StartZ=0 EndX=-3.67543 EndY=1.2 EndZ=0
    g1: LineSegment StartX=-3.67543 StartY=1.2 StartZ=0 EndX=-3.67543 EndY=-1.2 EndZ=0
    g2: LineSegment StartX=-3.67543 StartY=-1.2 StartZ=0 EndX=-2.67543 EndY=-1.2 EndZ=0
    g3: LineSegment StartX=-2.67543 StartY=-1.2 StartZ=0 EndX=-3.17543 EndY=-1 EndZ=0
    g4: LineSegment StartX=-3.17543 StartY=-1 StartZ=0 EndX=-3.17543 EndY=1 EndZ=0
    g5: LineSegment StartX=-3.17543 StartY=1 StartZ=0 EndX=-2.67543 EndY=1.2 EndZ=0
  constraints (15):
    c: Horizontal(g0)
    c: Coincident(g0,g1)
    c: Coincident(g1,g2)
    c: Coincident(g2,g3)
    c: Coincident(g3,g4)
    c: Coincident(g4,g5)
    c: Coincident(g5,g0)
    c: Symmetric(g4,g3,g-1)
    c: Symmetric(g0,g2,g-1)
    c: Symmetric(g1,g0,g-1)
    c: DistanceX(g0,g4) = 0.5
    c: DistanceY(g3,g4) = 2
    c: DistanceY(g1,g0) = 2.4
    c: PointOnObject(g3,g-3)
    c: DistanceX(g4,g0) = 0.5
FEATURE [PartDesign::Groove] Groove212  label="M3 Nut Smooth204"
  Angle = 360
  Axis = (-2e-16,3e-16,1)
  Base = (0,0,0)
  BaseFeature = -> Pad1031
  Profile = -> Sketch021
  ReferenceAxis = -> Sketch021 [V_Axis]
  Reversed = true
FEATURE [PartDesign::Groove] Groove214  label="M3 Nut Smooth206"
  Angle = 360
  Axis = (-2e-16,3e-16,1)
  Base = (0,0,0)
  BaseFeature = -> Pad006
  Profile = -> Sketch068
  ReferenceAxis = -> Sketch068 [V_Axis]
  Reversed = true
FEATURE [PartDesign::Pad] Pad1032  label="Baseplate042"
  Length = 12
  Length2 = 100
  Profile = -> Sketch060
  Type = 0
FEATURE [Sketcher::SketchObject] Sketch062
  MapMode = 5
  Placement = pos=(0,-23.75,0) rot=(1,0,0;1.5708rad)
  Support = -> [Pad1032]
  sketch-geometry (2):
    g0: Circle CenterX=-5 CenterY=6 CenterZ=0 NormalX=0 NormalY=0 NormalZ=1 AngleXU=0 Radius=1.6
    g1: Circle CenterX=5 CenterY=6 CenterZ=0 NormalX=0 NormalY=0 NormalZ=1 AngleXU=0 Radius=1.6
  constraints (5):
    c: Symmetric(g0,g1,g-2)
    c: Equal(g0,g1)
    c: Radius(g1) = 1.6
    c: DistanceY(g-1,g0) = 6
    c: DistanceX(g0,g1) = 10
FEATURE [PartDesign::Pocket] Pocket818  label="Screwholes Front002"
  BaseFeature = -> Pad1032
  Length = 10
  Length2 = 100
  Profile = -> Sketch062
  Type = 0
FEATURE [Sketcher::SketchObject] Sketch054
  MapMode = 5
  Placement = pos=(0,23.75,0) rot=(0,0.707107,0.707107;3.14159rad)
  Support = -> [Pocket818]
  sketch-geometry (2):
    g0: Circle CenterX=-5 CenterY=6 CenterZ=0 NormalX=0 NormalY=0 NormalZ=1 AngleXU=0 Radius=1.6
    g1: Circle CenterX=5 CenterY=6 CenterZ=0 NormalX=0 NormalY=0 NormalZ=1 AngleXU=0 Radius=1.6
  constraints (5):
    c: Symmetric(g0,g1,g-2)
    c: Equal(g0,g1)
    c: Radius(g1) = 1.6
    c: DistanceY(g-1,g0) = 6
    c: DistanceX(g0,g1) = 10
FEATURE [PartDesign::Pocket] Pocket819  label="Screwholes Rear003"
  BaseFeature = -> Pocket818
  Length = 10
  Length2 = 100
  Profile = -> Sketch054
  Type = 0
FEATURE [Sketcher::SketchObject] Sketch055
  MapMode = 5
  Placement = pos=(0,0,12) rot=(0,0,1;0rad)
  Support = -> [Pocket819]
  sketch-geometry (16):
    g0: LineSegment StartX=-7.9 StartY=20.75 StartZ=0 EndX=-2.1 EndY=20.75 EndZ=0
    g1: LineSegment StartX=-2.1 StartY=20.75 StartZ=0 EndX=-2.1 EndY=17.75 EndZ=0
    g2: LineSegment StartX=-2.1 StartY=17.75 StartZ=0 EndX=-7.9 EndY=17.75 EndZ=0
    g3: LineSegment StartX=-7.9 StartY=17.75 StartZ=0 EndX=-7.9 EndY=20.75 EndZ=0
    g4: LineSegment StartX=2.1 StartY=20.75 StartZ=0 EndX=7.9 EndY=20.75 EndZ=0
    g5: LineSegment StartX=7.9 StartY=20.75 StartZ=0 EndX=7.9 EndY=17.75 EndZ=0
    g6: LineSegment StartX=7.9 StartY=17.75 StartZ=0 EndX=2.1 EndY=17.75 EndZ=0
    g7: LineSegment StartX=2.1 StartY=17.75 StartZ=0 EndX=2.1 EndY=20.75 EndZ=0
    g8: LineSegment StartX=-7.9 StartY=-17.75 StartZ=0 EndX=-2.1 EndY=-17.75 EndZ=0
    g9: LineSegment StartX=-2.1 StartY=-17.75 StartZ=0 EndX=-2.1 EndY=-20.75 EndZ=0
    g10: LineSegment StartX=-2.1 StartY=-20.75 StartZ=0 EndX=-7.9 EndY=-20.75 EndZ=0
    g11: LineSegment StartX=-7.9 StartY=-20.75 StartZ=0 EndX=-7.9 EndY=-17.75 EndZ=0
    g12: LineSegment StartX=2.1 StartY=-17.75 StartZ=0 EndX=7.9 EndY=-17.75 EndZ=0
    g13: LineSegment StartX=7.9 StartY=-17.75 StartZ=0 EndX=7.9 EndY=-20.75 EndZ=0
    g14: LineSegment StartX=7.9 StartY=-20.75 StartZ=0 EndX=2.1 EndY=-20.75 EndZ=0
    g15: LineSegment StartX=2.1 StartY=-20.75 StartZ=0 EndX=2.1 EndY=-17.75 EndZ=0
  constraints (45):
    c: Coincident(g0,g1)
    c: Coincident(g1,g2)
    c: Coincident(g2,g3)
    c: Coincident(g3,g0)
    c: Horizontal(g0)
    c: Horizontal(g2)
    c: Vertical(g1)
    c: Vertical(g3)
    c: Coincident(g4,g5)
    c: Coincident(g5,g6)
    c: Coincident(g6,g7)
    c: Coincident(g7,g4)
    c: Horizontal(g4)
    c: Horizontal(g6)
    c: Vertical(g5)
    c: Vertical(g7)
    c: Coincident(g8,g9)
    c: Coincident(g9,g10)
    c: Coincident(g10,g11)
    c: Coincident(g11,g8)
    c: Horizontal(g8)
    c: Horizontal(g10)
    c: Vertical(g9)
    c: Vertical(g11)
    c: Coincident(g12,g13)
    c: Coincident(g13,g14)
    c: Coincident(g14,g15)
    c: Coincident(g15,g12)
    c: Horizontal(g12)
    c: Horizontal(g14)
    c: Vertical(g13)
    c: Vertical(g15)
    c: Equal(g11,g13)
    c: Equal(g13,g5)
    c: Equal(g5,g3)
    c: Equal(g0,g4)
    c: Equal(g4,g10)
    c: Equal(g10,g14)
    c: DistanceX(g0,g0) = 5.8
    c: Symmetric(g0,g4,g-2)
    c: Symmetric(g9,g14,g-2)
    c: Symmetric(g12,g5,g-1)
    c: DistanceY(g10,g-1) = 20.75
    c: DistanceY(g11,g11) = 3
    c: DistanceX(g0,g4) = 4.2
FEATURE [PartDesign::Pocket] Pocket817  label="Nutholes Front and Rear002"
  BaseFeature = -> Pocket819
  Length = 12
  Length2 = 100
  Profile = -> Sketch055
  Type = 0
FEATURE [Sketcher::SketchObject] Sketch051
  MapMode = 5
  Placement = pos=(0,0,12) rot=(0,0,1;0rad)
  Support = -> [Pocket817]
  sketch-geometry (4):
    g0: Circle CenterX=-5 CenterY=5 CenterZ=0 NormalX=0 NormalY=0 NormalZ=1 AngleXU=0 Radius=1.6
    g1: Circle CenterX=5 CenterY=5 CenterZ=0 NormalX=0 NormalY=0 NormalZ=1 AngleXU=0 Radius=1.6
    g2: Circle CenterX=-5 CenterY=-5 CenterZ=0 NormalX=0 NormalY=0 NormalZ=1 AngleXU=0 Radius=1.6
    g3: Circle CenterX=5 CenterY=-5 CenterZ=0 NormalX=0 NormalY=0 NormalZ=1 AngleXU=0 Radius=1.6
  constraints (9):
    c: Equal(g0,g1)
    c: Equal(g1,g2)
    c: Equal(g2,g3)
    c: Symmetric(g3,g1,g-1)
    c: Symmetric(g0,g1,g-2)
    c: Symmetric(g2,g3,g-2)
    c: Radius(g1) = 1.6
    c: DistanceX(g0,g1) = 10
    c: DistanceY(g2,g0) = 10
FEATURE [PartDesign::Pocket] Pocket820  label="Screwholes Covers"
  BaseFeature = -> Pocket817
  Length = 12
  Length2 = 100
  Profile = -> Sketch051
  Type = 0
FEATURE [Sketcher::SketchObject] Sketch056
  ExternalGeometry = -> [Pocket820]
  MapMode = 5
  Placement = pos=(0,0,12) rot=(0,0,1;0rad)
  Support = -> [Pocket820]
  sketch-geometry (28):
    g0: LineSegment StartX=-5 StartY=8.2909 StartZ=0 EndX=-7.85 EndY=6.64545 EndZ=0
    g1: LineSegment StartX=-7.85 StartY=6.64545 StartZ=0 EndX=-7.85 EndY=3.35455 EndZ=0
    g2: LineSegment StartX=-7.85 StartY=3.35455 StartZ=0 EndX=-5 EndY=1.7091 EndZ=0
    g3: LineSegment StartX=-5 StartY=1.7091 StartZ=0 EndX=-2.15 EndY=3.35455 EndZ=0
    g4: LineSegment StartX=-2.15 StartY=3.35455 StartZ=0 EndX=-2.15 EndY=6.64545 EndZ=0
    g5: LineSegment StartX=-2.15 StartY=6.64545 StartZ=0 EndX=-5 EndY=8.2909 EndZ=0
    g6: Circle [constr] CenterX=-5 CenterY=5 CenterZ=0 NormalX=0 NormalY=0 NormalZ=1 AngleXU=0 Radius=3.2909
    g7: LineSegment StartX=7.85 StartY=6.64545 StartZ=0 EndX=5 EndY=8.2909 EndZ=0
    g8: LineSegment StartX=5 StartY=8.2909 StartZ=0 EndX=2.15 EndY=6.64545 EndZ=0
    g9: LineSegment StartX=2.15 StartY=6.64545 StartZ=0 EndX=2.15 EndY=3.35455 EndZ=0
    g10: LineSegment StartX=2.15 StartY=3.35455 StartZ=0 EndX=5 EndY=1.7091 EndZ=0
    g11: LineSegment StartX=5 StartY=1.7091 StartZ=0 EndX=7.85 EndY=3.35455 EndZ=0
    g12: LineSegment StartX=7.85 StartY=3.35455 StartZ=0 EndX=7.85 EndY=6.64545 EndZ=0
    g13: Circle [constr] CenterX=5 CenterY=5 CenterZ=0 NormalX=0 NormalY=0 NormalZ=1 AngleXU=0 Radius=3.2909
    g14: LineSegment StartX=-5 StartY=-1.7091 StartZ=0 EndX=-7.85 EndY=-3.35455 EndZ=0
    g15: LineSegment StartX=-7.85 StartY=-3.35455 StartZ=0 EndX=-7.85 EndY=-6.64545 EndZ=0
    g16: LineSegment StartX=-7.85 StartY=-6.64545 StartZ=0 EndX=-5 EndY=-8.2909 EndZ=0
    g17: LineSegment StartX=-5 StartY=-8.2909 StartZ=0 EndX=-2.15 EndY=-6.64545 EndZ=0
    g18: LineSegment StartX=-2.15 StartY=-6.64545 StartZ=0 EndX=-2.15 EndY=-3.35455 EndZ=0
    g19: LineSegment StartX=-2.15 StartY=-3.35455 StartZ=0 EndX=-5 EndY=-1.7091 EndZ=0
    g20: Circle [constr] CenterX=-5 CenterY=-5 CenterZ=0 NormalX=0 NormalY=0 NormalZ=1 AngleXU=0 Radius=3.2909
    g21: LineSegment StartX=7.85 StartY=-3.35455 StartZ=0 EndX=5 EndY=-1.7091 EndZ=0
    g22: LineSegment StartX=5 StartY=-1.7091 StartZ=0 EndX=2.15 EndY=-3.35455 EndZ=0
    g23: LineSegment StartX=2.15 StartY=-3.35455 StartZ=0 EndX=2.15 EndY=-6.64545 EndZ=0
    g24: LineSegment StartX=2.15 StartY=-6.64545 StartZ=0 EndX=5 EndY=-8.2909 EndZ=0
    g25: LineSegment StartX=5 StartY=-8.2909 StartZ=0 EndX=7.85 EndY=-6.64545 EndZ=0
    g26: LineSegment StartX=7.85 StartY=-6.64545 StartZ=0 EndX=7.85 EndY=-3.35455 EndZ=0
    g27: Circle [constr] CenterX=5 CenterY=-5 CenterZ=0 NormalX=0 NormalY=0 NormalZ=1 AngleXU=0 Radius=3.2909
  constraints (64):
    c: Coincident(g0,g1)
    c: Coincident(g1,g2)
    c: Coincident(g2,g3)
    c: Coincident(g3,g4)
    c: Coincident(g4,g5)
    c: Coincident(g5,g0)
    c: Equal(g0, g1-g5) x5
    c: PointOnObject(g0,g6)
    c: PointOnObject(g1,g6)
    c: PointOnObject(g2,g6)
    c: PointOnObject(g3,g6)
    c: PointOnObject(g4,g6)
    c: PointOnObject(g5,g6)
    c: Coincident(g7,g8)
    c: Coincident(g8,g9)
    c: Coincident(g9,g10)
    c: Coincident(g10,g11)
    c: Coincident(g11,g12)
    c: Coincident(g12,g7)
    c: Equal(g7, g8-g12) x5
    c: PointOnObject(g7,g13)
    c: PointOnObject(g8,g13)
    c: PointOnObject(g9,g13)
    c: PointOnObject(g10,g13)
    c: PointOnObject(g11,g13)
    c: PointOnObject(g12,g13)
    c: Coincident(g14,g15)
    c: Coincident(g15,g16)
    c: Coincident(g16,g17)
    c: Coincident(g17,g18)
    c: Coincident(g18,g19)
    c: Coincident(g19,g14)
    c: Equal(g14, g15-g19) x5
    c: PointOnObject(g14,g20)
    c: PointOnObject(g15,g20)
    c: PointOnObject(g16,g20)
    c: PointOnObject(g17,g20)
    c: PointOnObject(g18,g20)
    c: PointOnObject(g19,g20)
    c: Coincident(g21,g22)
    c: Coincident(g22,g23)
    c: Coincident(g23,g24)
    c: Coincident(g24,g25)
    c: Coincident(g25,g26)
    c: Coincident(g26,g21)
    c: Equal(g21, g22-g26) x5
    c: PointOnObject(g21,g27)
    c: PointOnObject(g22,g27)
    c: PointOnObject(g23,g27)
    c: PointOnObject(g24,g27)
    c: PointOnObject(g25,g27)
    c: PointOnObject(g26,g27)
    c: Equal(g20,g6)
    c: Equal(g6,g13)
    c: Equal(g13,g27)
    c: Coincident(g6,g-3)
    c: Coincident(g13,g-4)
    c: Coincident(g20,g-6)
    c: Coincident(g27,g-5)
    c: Vertical(g15)
    c: Vertical(g1)
    c: Vertical(g12)
    c: Vertical(g26)
    c: Distance(g23,g25) = 5.7
FEATURE [PartDesign::Pad] Pad1033  label="M3 Nut Primitive206"
  Length = 1.2
  Length2 = 1.2
  Profile = -> Sketch022
  Type = 4
FEATURE [Sketcher::SketchObject] Sketch064
  ExternalGeometry = -> [Pad1033]
  MapMode = 5
  Placement = pos=(0,0,0) rot=(0.57735,0.57735,0.57735;2.0944rad)
  Support = -> [YZ_Plane956]
  sketch-geometry (6):
    g0: LineSegment StartX=-2.67543 StartY=1.2 StartZ=0 EndX=-3.67543 EndY=1.2 EndZ=0
    g1: LineSegment StartX=-3.67543 StartY=1.2 StartZ=0 EndX=-3.67543 EndY=-1.2 EndZ=0
    g2: LineSegment StartX=-3.67543 StartY=-1.2 StartZ=0 EndX=-2.67543 EndY=-1.2 EndZ=0
    g3: LineSegment StartX=-2.67543 StartY=-1.2 StartZ=0 EndX=-3.17543 EndY=-1 EndZ=0
    g4: LineSegment StartX=-3.17543 StartY=-1 StartZ=0 EndX=-3.17543 EndY=1 EndZ=0
    g5: LineSegment StartX=-3.17543 StartY=1 StartZ=0 EndX=-2.67543 EndY=1.2 EndZ=0
  constraints (15):
    c: Horizontal(g0)
    c: Coincident(g0,g1)
    c: Coincident(g1,g2)
    c: Coincident(g2,g3)
    c: Coincident(g3,g4)
    c: Coincident(g4,g5)
    c: Coincident(g5,g0)
    c: Symmetric(g4,g3,g-1)
    c: Symmetric(g0,g2,g-1)
    c: Symmetric(g1,g0,g-1)
    c: DistanceX(g0,g4) = 0.5
    c: DistanceY(g3,g4) = 2
    c: DistanceY(g1,g0) = 2.4
    c: PointOnObject(g3,g-3)
    c: DistanceX(g4,g0) = 0.5
FEATURE [PartDesign::Groove] Groove213  label="M3 Nut Smooth205"
  Angle = 360
  Axis = (-2e-16,3e-16,1)
  Base = (0,0,0)
  BaseFeature = -> Pad1033
  Profile = -> Sketch064
  ReferenceAxis = -> Sketch064 [V_Axis]
  Reversed = true
FEATURE [PartDesign::Pocket] Pocket821  label="Nutholes Covers"
  BaseFeature = -> Pocket820
  Length = 9
  Length2 = 100
  Profile = -> Sketch056
  Type = 0
FEATURE [PartDesign::Pocket] Pocket027  label="Screwholes Front003"
  BaseFeature = -> Pad1030
  Length = 10
  Length2 = 100
  Profile = -> Sketch2361
  Type = 0
FEATURE [Sketcher::SketchObject] Sketch2359
  MapMode = 5
  Placement = pos=(0,23.75,0) rot=(0,0.707107,0.707107;3.14159rad)
  Support = -> [Pocket027]
  sketch-geometry (2):
    g0: Circle CenterX=-15 CenterY=6 CenterZ=0 NormalX=0 NormalY=0 NormalZ=1 AngleXU=0 Radius=1.6
    g1: Circle CenterX=15 CenterY=6 CenterZ=0 NormalX=0 NormalY=0 NormalZ=1 AngleXU=0 Radius=1.6
  constraints (5):
    c: Symmetric(g0,g1,g-2)
    c: Equal(g0,g1)
    c: Radius(g1) = 1.6
    c: DistanceY(g-1,g0) = 6
    c: DistanceX(g0,g1) = 30
FEATURE [PartDesign::Pocket] Pocket816  label="Screwholes Rear002"
  BaseFeature = -> Pocket027
  Length = 10
  Length2 = 100
  Profile = -> Sketch2359
  Type = 0
FEATURE [Sketcher::SketchObject] Sketch061
  MapMode = 5
  Placement = pos=(0,0,12) rot=(0,0,1;0rad)
  Support = -> [Pocket816]
  sketch-geometry (16):
    g0: LineSegment StartX=-17.9 StartY=20.75 StartZ=0 EndX=-12.1 EndY=20.75 EndZ=0
    g1: LineSegment StartX=-12.1 StartY=20.75 StartZ=0 EndX=-12.1 EndY=17.75 EndZ=0
    g2: LineSegment StartX=-12.1 StartY=17.75 StartZ=0 EndX=-17.9 EndY=17.75 EndZ=0
    g3: LineSegment StartX=-17.9 StartY=17.75 StartZ=0 EndX=-17.9 EndY=20.75 EndZ=0
    g4: LineSegment StartX=12.1 StartY=20.75 StartZ=0 EndX=17.9 EndY=20.75 EndZ=0
    g5: LineSegment StartX=17.9 StartY=20.75 StartZ=0 EndX=17.9 EndY=17.75 EndZ=0
    g6: LineSegment StartX=17.9 StartY=17.75 StartZ=0 EndX=12.1 EndY=17.75 EndZ=0
    g7: LineSegment StartX=12.1 StartY=17.75 StartZ=0 EndX=12.1 EndY=20.75 EndZ=0
    g8: LineSegment StartX=-17.9 StartY=-17.75 StartZ=0 EndX=-12.1 EndY=-17.75 EndZ=0
    g9: LineSegment StartX=-12.1 StartY=-17.75 StartZ=0 EndX=-12.1 EndY=-20.75 EndZ=0
    g10: LineSegment StartX=-12.1 StartY=-20.75 StartZ=0 EndX=-17.9 EndY=-20.75 EndZ=0
    g11: LineSegment StartX=-17.9 StartY=-20.75 StartZ=0 EndX=-17.9 EndY=-17.75 EndZ=0
    g12: LineSegment StartX=12.1 StartY=-17.75 StartZ=0 EndX=17.9 EndY=-17.75 EndZ=0
    g13: LineSegment StartX=17.9 StartY=-17.75 StartZ=0 EndX=17.9 EndY=-20.75 EndZ=0
    g14: LineSegment StartX=17.9 StartY=-20.75 StartZ=0 EndX=12.1 EndY=-20.75 EndZ=0
    g15: LineSegment StartX=12.1 StartY=-20.75 StartZ=0 EndX=12.1 EndY=-17.75 EndZ=0
  constraints (45):
    c: Coincident(g0,g1)
    c: Coincident(g1,g2)
    c: Coincident(g2,g3)
    c: Coincident(g3,g0)
    c: Horizontal(g0)
    c: Horizontal(g2)
    c: Vertical(g1)
    c: Vertical(g3)
    c: Coincident(g4,g5)
    c: Coincident(g5,g6)
    c: Coincident(g6,g7)
    c: Coincident(g7,g4)
    c: Horizontal(g4)
    c: Horizontal(g6)
    c: Vertical(g5)
    c: Vertical(g7)
    c: Coincident(g8,g9)
    c: Coincident(g9,g10)
    c: Coincident(g10,g11)
    c: Coincident(g11,g8)
    c: Horizontal(g8)
    c: Horizontal(g10)
    c: Vertical(g9)
    c: Vertical(g11)
    c: Coincident(g12,g13)
    c: Coincident(g13,g14)
    c: Coincident(g14,g15)
    c: Coincident(g15,g12)
    c: Horizontal(g12)
    c: Horizontal(g14)
    c: Vertical(g13)
    c: Vertical(g15)
    c: Equal(g11,g13)
    c: Equal(g13,g5)
    c: Equal(g5,g3)
    c: Equal(g0,g4)
    c: Equal(g4,g10)
    c: Equal(g10,g14)
    c: DistanceX(g0,g0) = 5.8
    c: Symmetric(g0,g4,g-2)
    c: Symmetric(g9,g14,g-2)
    c: Symmetric(g12,g5,g-1)
    c: DistanceY(g10,g-1) = 20.75
    c: DistanceY(g11,g11) = 3
    c: DistanceX(g0,g4) = 24.2
FEATURE [PartDesign::Pocket] Pocket028  label="Nutholes Front and Rear003"
  BaseFeature = -> Pocket816
  Length = 12
  Length2 = 100
  Profile = -> Sketch061
  Type = 0
FEATURE [Sketcher::SketchObject] Sketch2360
  MapMode = 5
  Placement = pos=(0,0,12) rot=(0,0,1;0rad)
  Support = -> [Pocket028]
  sketch-geometry (4):
    g0: Circle CenterX=-15 CenterY=5 CenterZ=0 NormalX=0 NormalY=0 NormalZ=1 AngleXU=0 Radius=1.6
    g1: Circle CenterX=15 CenterY=5 CenterZ=0 NormalX=0 NormalY=0 NormalZ=1 AngleXU=0 Radius=1.6
    g2: Circle CenterX=-15 CenterY=-5 CenterZ=0 NormalX=0 NormalY=0 NormalZ=1 AngleXU=0 Radius=1.6
    g3: Circle CenterX=15 CenterY=-5 CenterZ=0 NormalX=0 NormalY=0 NormalZ=1 AngleXU=0 Radius=1.6
  constraints (9):
    c: Equal(g0,g1)
    c: Equal(g1,g2)
    c: Equal(g2,g3)
    c: Symmetric(g3,g1,g-1)
    c: Symmetric(g0,g1,g-2)
    c: Symmetric(g2,g3,g-2)
    c: Radius(g1) = 1.6
    c: DistanceX(g0,g1) = 30
    c: DistanceY(g2,g0) = 10
FEATURE [PartDesign::Pocket] Pocket030  label="Screwholes Covers001"
  BaseFeature = -> Pocket028
  Length = 12
  Length2 = 100
  Profile = -> Sketch2360
  Type = 0
FEATURE [Sketcher::SketchObject] Sketch065
  ExternalGeometry = -> [Pocket030]
  MapMode = 5
  Placement = pos=(0,0,12) rot=(0,0,1;0rad)
  Support = -> [Pocket030]
  sketch-geometry (28):
    g0: LineSegment StartX=-15 StartY=8.2909 StartZ=0 EndX=-17.85 EndY=6.64545 EndZ=0
    g1: LineSegment StartX=-17.85 StartY=6.64545 StartZ=0 EndX=-17.85 EndY=3.35455 EndZ=0
    g2: LineSegment StartX=-17.85 StartY=3.35455 StartZ=0 EndX=-15 EndY=1.7091 EndZ=0
    g3: LineSegment StartX=-15 StartY=1.7091 StartZ=0 EndX=-12.15 EndY=3.35455 EndZ=0
    g4: LineSegment StartX=-12.15 StartY=3.35455 StartZ=0 EndX=-12.15 EndY=6.64545 EndZ=0
    g5: LineSegment StartX=-12.15 StartY=6.64545 StartZ=0 EndX=-15 EndY=8.2909 EndZ=0
    g6: Circle [constr] CenterX=-15 CenterY=5 CenterZ=0 NormalX=0 NormalY=0 NormalZ=1 AngleXU=0 Radius=3.2909
    g7: LineSegment StartX=15 StartY=8.2909 StartZ=0 EndX=12.15 EndY=6.64545 EndZ=0
    g8: LineSegment StartX=12.15 StartY=6.64545 StartZ=0 EndX=12.15 EndY=3.35455 EndZ=0
    g9: LineSegment StartX=12.15 StartY=3.35455 StartZ=0 EndX=15 EndY=1.7091 EndZ=0
    g10: LineSegment StartX=15 StartY=1.7091 StartZ=0 EndX=17.85 EndY=3.35455 EndZ=0
    g11: LineSegment StartX=17.85 StartY=3.35455 StartZ=0 EndX=17.85 EndY=6.64545 EndZ=0
    g12: LineSegment StartX=17.85 StartY=6.64545 StartZ=0 EndX=15 EndY=8.2909 EndZ=0
    g13: Circle [constr] CenterX=15 CenterY=5 CenterZ=0 NormalX=0 NormalY=0 NormalZ=1 AngleXU=0 Radius=3.2909
    g14: LineSegment StartX=-15 StartY=-1.7091 StartZ=0 EndX=-17.85 EndY=-3.35455 EndZ=0
    g15: LineSegment StartX=-17.85 StartY=-3.35455 StartZ=0 EndX=-17.85 EndY=-6.64545 EndZ=0
    g16: LineSegment StartX=-17.85 StartY=-6.64545 StartZ=0 EndX=-15 EndY=-8.2909 EndZ=0
    g17: LineSegment StartX=-15 StartY=-8.2909 StartZ=0 EndX=-12.15 EndY=-6.64545 EndZ=0
    g18: LineSegment StartX=-12.15 StartY=-6.64545 StartZ=0 EndX=-12.15 EndY=-3.35455 EndZ=0
    g19: LineSegment StartX=-12.15 StartY=-3.35455 StartZ=0 EndX=-15 EndY=-1.7091 EndZ=0
    g20: Circle [constr] CenterX=-15 CenterY=-5 CenterZ=0 NormalX=0 NormalY=0 NormalZ=1 AngleXU=0 Radius=3.2909
    g21: LineSegment StartX=15 StartY=-1.7091 StartZ=0 EndX=12.15 EndY=-3.35455 EndZ=0
    g22: LineSegment StartX=12.15 StartY=-3.35455 StartZ=0 EndX=12.15 EndY=-6.64545 EndZ=0
    g23: LineSegment StartX=12.15 StartY=-6.64545 StartZ=0 EndX=15 EndY=-8.2909 EndZ=0
    g24: LineSegment StartX=15 StartY=-8.2909 StartZ=0 EndX=17.85 EndY=-6.64545 EndZ=0
    g25: LineSegment StartX=17.85 StartY=-6.64545 StartZ=0 EndX=17.85 EndY=-3.35455 EndZ=0
    g26: LineSegment StartX=17.85 StartY=-3.35455 StartZ=0 EndX=15 EndY=-1.7091 EndZ=0
    g27: Circle [constr] CenterX=15 CenterY=-5 CenterZ=0 NormalX=0 NormalY=0 NormalZ=1 AngleXU=0 Radius=3.2909
  constraints (64):
    c: Coincident(g0,g1)
    c: Coincident(g1,g2)
    c: Coincident(g2,g3)
    c: Coincident(g3,g4)
    c: Coincident(g4,g5)
    c: Coincident(g5,g0)
    c: Equal(g0, g1-g5) x5
    c: PointOnObject(g0,g6)
    c: PointOnObject(g1,g6)
    c: PointOnObject(g2,g6)
    c: PointOnObject(g3,g6)
    c: PointOnObject(g4,g6)
    c: PointOnObject(g5,g6)
    c: Coincident(g7,g8)
    c: Coincident(g8,g9)
    c: Coincident(g9,g10)
    c: Coincident(g10,g11)
    c: Coincident(g11,g12)
    c: Coincident(g12,g7)
    c: Equal(g7, g8-g12) x5
    c: PointOnObject(g7,g13)
    c: PointOnObject(g8,g13)
    c: PointOnObject(g9,g13)
    c: PointOnObject(g10,g13)
    c: PointOnObject(g11,g13)
    c: PointOnObject(g12,g13)
    c: Coincident(g14,g15)
    c: Coincident(g15,g16)
    c: Coincident(g16,g17)
    c: Coincident(g17,g18)
    c: Coincident(g18,g19)
    c: Coincident(g19,g14)
    c: Equal(g14, g15-g19) x5
    c: PointOnObject(g14,g20)
    c: PointOnObject(g15,g20)
    c: PointOnObject(g16,g20)
    c: PointOnObject(g17,g20)
    c: PointOnObject(g18,g20)
    c: PointOnObject(g19,g20)
    c: Coincident(g21,g22)
    c: Coincident(g22,g23)
    c: Coincident(g23,g24)
    c: Coincident(g24,g25)
    c: Coincident(g25,g26)
    c: Coincident(g26,g21)
    c: Equal(g21, g22-g26) x5
    c: PointOnObject(g21,g27)
    c: PointOnObject(g22,g27)
    c: PointOnObject(g23,g27)
    c: PointOnObject(g24,g27)
    c: PointOnObject(g25,g27)
    c: PointOnObject(g26,g27)
    c: Coincident(g13,g-5)
    c: Coincident(g27,g-6)
    c: Coincident(g6,g-3)
    c: Coincident(g20,g-4)
    c: Equal(g6,g20)
    c: Equal(g20,g13)
    c: Equal(g13,g27)
    c: Vertical(g1)
    c: Vertical(g15)
    c: Vertical(g8)
    c: Vertical(g22)
    c: Distance(g4,g0) = 5.7
FEATURE [PartDesign::Pocket] Pocket029  label="Nutholes Covers001"
  BaseFeature = -> Pocket030
  Length = 9
  Length2 = 100
  Profile = -> Sketch065
  Type = 0
FEATURE [PartDesign::Pad] Pad040  label="M3 Nut Primitive210"
  Length = 1.2
  Length2 = 1.2
  Profile = -> Sketch070
  Type = 4
FEATURE [PartDesign::Chamfer] Chamfer004  label="M3 Nut Smooth Hole204"
  Base = -> Groove214 [Edge24,Edge23]
  BaseFeature = -> Groove214
  Size = 0.2
FEATURE [PartDesign::Chamfer] Chamfer009  label="M3x8 Smooth157"
  Base = -> Pocket017 [Face11,Edge2,Edge24,Edge3]
  BaseFeature = -> Pocket017
  Size = 0.2
FEATURE [PartDesign::Fillet] Fillet014  label="Smooth Baseplate Corners004"
  Base = -> Pocket029 [Edge7,Edge74,Edge4,Edge1]
  BaseFeature = -> Pocket029
  Radius = 0.4
FEATURE [PartDesign::Chamfer] Chamfer010  label="M3x8 Smooth002"
  Base = -> Pocket019 [Face11,Edge2,Edge24,Edge3]
  BaseFeature = -> Pocket019
  Size = 0.2
FEATURE [PartDesign::Fillet] Fillet256  label="Screwheads Top Fillet"
  Base = -> Pocket023 [Edge87,Edge89,Edge90,Edge92,Edge4,Edge6,Edge8,Edge10]
  BaseFeature = -> Pocket023
  Radius = 1
FEATURE [Sketcher::SketchObject] Sketch053
  MapMode = 5
  Placement = pos=(0,0,0) rot=(1,0,0;3.14159rad)
  Support = -> [Fillet256]
  sketch-geometry (4):
    g0: Circle CenterX=-5 CenterY=-6 CenterZ=0 NormalX=0 NormalY=0 NormalZ=1 AngleXU=0 Radius=2.85
    g1: Circle CenterX=5 CenterY=-6 CenterZ=0 NormalX=0 NormalY=0 NormalZ=1 AngleXU=0 Radius=2.85
    g2: Circle CenterX=-15 CenterY=-64 CenterZ=0 NormalX=0 NormalY=0 NormalZ=1 AngleXU=0 Radius=2.85
    g3: Circle CenterX=15 CenterY=-64 CenterZ=0 NormalX=0 NormalY=0 NormalZ=1 AngleXU=0 Radius=2.85
  constraints (10):
    c: Symmetric(g0,g1,g-2)
    c: Symmetric(g2,g3,g-2)
    c: Equal(g0,g1)
    c: Equal(g1,g2)
    c: Equal(g2,g3)
    c: Radius(g1) = 2.85
    c: DistanceX(g0,g1) = 10
    c: DistanceX(g2,g3) = 30
    c: DistanceY(g1,g-1) = 6
    c: DistanceY(g2,g-1) = 64
FEATURE [PartDesign::Pocket] Pocket021  label="Screwheads Bottom"
  BaseFeature = -> Fillet256
  Length = 2
  Length2 = 100
  Profile = -> Sketch053
  Type = 0
FEATURE [PartDesign::Chamfer] Chamfer508  label="M3 Nut Smooth Hole205"
  Base = -> Groove211 [Edge24,Edge23]
  BaseFeature = -> Groove211
  Size = 0.2
FEATURE [PartDesign::Chamfer] Chamfer509  label="M3 Nut Smooth Hole206"
  Base = -> Groove212 [Edge24,Edge23]
  BaseFeature = -> Groove212
  Size = 0.2
FEATURE [PartDesign::Chamfer] Chamfer014  label="Screwheads Bottom Chamfer004"
  Base = -> Pocket021 [Edge136,Edge138,Edge148,Edge150]
  BaseFeature = -> Pocket021
  Size = 1.2
FEATURE [Sketcher::SketchObject] Sketch050
  MapMode = 5
  Placement = pos=(0,0,5) rot=(0,0,1;0rad)
  Support = -> [Chamfer014]
  sketch-geometry (2):
    g0: Circle CenterX=-39 CenterY=44 CenterZ=0 NormalX=0 NormalY=0 NormalZ=1 AngleXU=0 Radius=8.15
    g1: Circle CenterX=39 CenterY=44 CenterZ=0 NormalX=0 NormalY=0 NormalZ=1 AngleXU=0 Radius=8.15
  constraints (5):
    c: Symmetric(g0,g1,g-2)
    c: DistanceX(g0,g1) = 78
    c: DistanceY(g-1,g0) = 44
    c: Radius(g0) = 8.15
    c: Equal(g0,g1)
FEATURE [PartDesign::Pocket] Pocket026  label="Ball Bearing Flange004"
  BaseFeature = -> Chamfer014
  Length = 4
  Length2 = 100
  Profile = -> Sketch050
  Type = 0
FEATURE [Sketcher::SketchObject] Sketch059
  MapMode = 5
  Placement = pos=(0,0,1) rot=(0,0,1;0rad)
  Support = -> [Pocket026]
  sketch-geometry (2):
    g0: Circle CenterX=-39 CenterY=44 CenterZ=0 NormalX=0 NormalY=0 NormalZ=1 AngleXU=0 Radius=6.15
    g1: Circle CenterX=39 CenterY=44 CenterZ=0 NormalX=0 NormalY=0 NormalZ=1 AngleXU=0 Radius=6.15
  constraints (5):
    c: Symmetric(g1,g0,g-2)
    c: DistanceX(g0,g1) = 78
    c: DistanceY(g-1,g0) = 44
    c: Radius(g0) = 6.15
    c: Equal(g0,g1)
FEATURE [PartDesign::Pocket] Pocket025  label="Ball Bearing004"
  BaseFeature = -> Pocket026
  Length = 1
  Length2 = 100
  Profile = -> Sketch059
  Type = 0
FEATURE [PartDesign::Chamfer] Chamfer012  label="M3 Nut Smooth Hole207"
  Base = -> Groove213 [Edge24,Edge23]
  BaseFeature = -> Groove213
  Size = 0.2
FEATURE [PartDesign::Fillet] Fillet257  label="Smooth Baseplate Corners003"
  Base = -> Pocket821 [Edge74,Edge7,Edge4,Edge1]
  BaseFeature = -> Pocket821
  Radius = 0.4
FEATURE [PartDesign::Chamfer] Chamfer013  label="M3x8 Smooth001"
  Base = -> Pocket018 [Face11,Edge2,Edge24,Edge3]
  BaseFeature = -> Pocket018
  Size = 0.2
FEATURE [PartDesign::Fillet] Fillet013  label="Smooth Nutholes Front and Rear001"
  Base = -> Fillet014 [Edge104,Edge120,Edge111,Edge98,Edge101,Edge118,Edge95,Edge109,Edge102,Edge119,Edge110,Edge96,Edge121,Edge112,Edge99,Edge105]
  BaseFeature = -> Fillet014
  Radius = 0.2
FEATURE [Sketcher::SketchObject] Sketch2362
  MapMode = 5
  Placement = pos=(0,0,12) rot=(0,0,1;0rad)
  Support = -> [Fillet013]
  sketch-geometry (8):
    g0: LineSegment StartX=-2.5 StartY=12.5 StartZ=0 EndX=2.5 EndY=12.5 EndZ=0
    g1: LineSegment StartX=7.5 StartY=7.5 StartZ=0 EndX=7.5 EndY=-7.5 EndZ=0
    g2: LineSegment StartX=2.5 StartY=-12.5 StartZ=0 EndX=-2.5 EndY=-12.5 EndZ=0
    g3: LineSegment StartX=-7.5 StartY=-7.5 StartZ=0 EndX=-7.5 EndY=7.5 EndZ=0
    g4: ArcOfCircle CenterX=-2.5 CenterY=7.5 CenterZ=0 NormalX=0 NormalY=0 NormalZ=1 AngleXU=0 Radius=5 StartAngle=1.5708 EndAngle=3.14159
    g5: ArcOfCircle CenterX=2.5 CenterY=7.5 CenterZ=0 NormalX=0 NormalY=0 NormalZ=1 AngleXU=0 Radius=5 StartAngle=1e-16 EndAngle=1.5708
    g6: ArcOfCircle CenterX=2.5 CenterY=-7.5 CenterZ=0 NormalX=0 NormalY=0 NormalZ=1 AngleXU=0 Radius=5 StartAngle=4.71239 EndAngle=6.28319
    g7: ArcOfCircle CenterX=-2.5 CenterY=-7.5 CenterZ=0 NormalX=0 NormalY=0 NormalZ=1 AngleXU=0 Radius=5 StartAngle=3.14159 EndAngle=4.71239
  constraints (18):
    c: Horizontal(g2)
    c: Vertical(g3)
    c: Tangent(g3,g4) = 1.5708
    c: Tangent(g0,g4) = 1.5708
    c: Tangent(g0,g5) = 1.5708
    c: Tangent(g1,g5) = 1.5708
    c: Tangent(g1,g6) = 1.5708
    c: Tangent(g2,g6) = 1.5708
    c: Tangent(g2,g7) = 1.5708
    c: Tangent(g3,g7) = 1.5708
    c: Equal(g5,g6)
    c: Equal(g6,g4)
    c: Equal(g4,g7)
    c: Symmetric(g1,g3,g-2)
    c: Symmetric(g0,g2,g-1)
    c: DistanceY(g2,g0) = 25
    c: DistanceX(g3,g1) = 15
    c: Radius(g7) = 5
FEATURE [PartDesign::Pocket] Pocket016  label="Accesshole007"
  BaseFeature = -> Fillet013
  Length = 12
  Length2 = 100
  Profile = -> Sketch2362
  Type = 0
FEATURE [PartDesign::Chamfer] Chamfer011  label="M3x8 Smooth003"
  Base = -> Pocket020 [Face11,Edge2,Edge24,Edge3]
  BaseFeature = -> Pocket020
  Size = 0.2
FEATURE [PartDesign::Fillet] Fillet012  label="Smooth Nutholes Front and Rear"
  Base = -> Fillet257 [Edge104,Edge98,Edge111,Edge116,Edge101,Edge95,Edge109,Edge114,Edge105,Edge99,Edge117,Edge112,Edge115,Edge110,Edge96,Edge102]
  BaseFeature = -> Fillet257
  Radius = 0.2
FEATURE [Sketcher::SketchObject] Sketch098
  MapMode = 5
  Support = -> [XY_Plane037]
  sketch-geometry (1):
    g0: Circle CenterX=0 CenterY=0 CenterZ=0 NormalX=0 NormalY=0 NormalZ=1 AngleXU=0 Radius=2.75
  constraints (2):
    c: Coincident(g0,g-1)
    c: Radius(g0) = 2.75
FEATURE [PartDesign::Pad] Pad031  label="M3x8 Head006"
  Length = 3
  Length2 = 100
  Profile = -> Sketch098
  Type = 0
FEATURE [Sketcher::SketchObject] Sketch089
  MapMode = 5
  Placement = pos=(0,0,3) rot=(0,0,1;0rad)
  Support = -> [Pad031]
  sketch-geometry (1):
    g0: Circle CenterX=0 CenterY=0 CenterZ=0 NormalX=0 NormalY=0 NormalZ=1 AngleXU=0 Radius=1.5
  constraints (2):
    c: Coincident(g0,g-1)
    c: Radius(g0) = 1.5
FEATURE [PartDesign::Pad] Pad033  label="M3x8 Thread154"
  BaseFeature = -> Pad031
  Length = 8
  Length2 = 100
  Profile = -> Sketch089
  Type = 0
FEATURE [Sketcher::SketchObject] Sketch090
  MapMode = 5
  Placement = pos=(0,0,0) rot=(1,0,0;3.14159rad)
  Support = -> [Pad033]
  sketch-geometry (7):
    g0: LineSegment StartX=1.275 StartY=0.736122 StartZ=0 EndX=0 EndY=1.47224 EndZ=0
    g1: LineSegment StartX=0 StartY=1.47224 StartZ=0 EndX=-1.275 EndY=0.736122 EndZ=0
    g2: LineSegment StartX=-1.275 StartY=0.736122 StartZ=0 EndX=-1.275 EndY=-0.736122 EndZ=0
    g3: LineSegment StartX=-1.275 StartY=-0.736122 StartZ=0 EndX=1.34766e-11 EndY=-1.47224 EndZ=0
    g4: LineSegment StartX=1.34766e-11 StartY=-1.47224 StartZ=0 EndX=1.275 EndY=-0.736122 EndZ=0
    g5: LineSegment StartX=1.275 StartY=-0.736122 StartZ=0 EndX=1.275 EndY=0.736122 EndZ=0
    g6: Circle [constr] CenterX=0 CenterY=0 CenterZ=0 NormalX=0 NormalY=0 NormalZ=1 AngleXU=0 Radius=1.47224
  constraints (16):
    c: Coincident(g0,g1)
    c: Coincident(g1,g2)
    c: Coincident(g2,g3)
    c: Coincident(g3,g4)
    c: Coincident(g4,g5)
    c: Coincident(g5,g0)
    c: Equal(g0, g1-g5) x5
    c: PointOnObject(g0,g6)
    c: PointOnObject(g1,g6)
    c: PointOnObject(g2,g6)
    c: PointOnObject(g3,g6)
    c: PointOnObject(g4,g6)
    c: PointOnObject(g5,g6)
    c: Coincident(g6,g-1)
    c: PointOnObject(g0,g-2)
    c: DistanceX(g1,g0) = 2.55
FEATURE [PartDesign::Pocket] Pocket033  label="M3x8 Wrench005"
  BaseFeature = -> Pad033
  Length = 1.3
  Length2 = 100
  Profile = -> Sketch090
  Type = 0
FEATURE [PartDesign::Chamfer] Chamfer516  label="M3x8 Smooth004"
  Base = -> Pocket033 [Face11,Edge2,Edge24,Edge3]
  BaseFeature = -> Pocket033
  Size = 0.2
FEATURE [Sketcher::SketchObject] Sketch088
  MapMode = 5
  Support = -> [XY_Plane031]
  sketch-geometry (1):
    g0: Circle CenterX=0 CenterY=0 CenterZ=0 NormalX=0 NormalY=0 NormalZ=1 AngleXU=0 Radius=2.75
  constraints (2):
    c: Coincident(g0,g-1)
    c: Radius(g0) = 2.75
FEATURE [PartDesign::Pad] Pad030  label="M3x8 Head005"
  Length = 3
  Length2 = 100
  Profile = -> Sketch088
  Type = 0
FEATURE [Sketcher::SketchObject] Sketch097
  MapMode = 5
  Placement = pos=(0,0,3) rot=(0,0,1;0rad)
  Support = -> [Pad030]
  sketch-geometry (1):
    g0: Circle CenterX=0 CenterY=0 CenterZ=0 NormalX=0 NormalY=0 NormalZ=1 AngleXU=0 Radius=1.5
  constraints (2):
    c: Coincident(g0,g-1)
    c: Radius(g0) = 1.5
FEATURE [PartDesign::Pad] Pad032  label="M3x8 Thread006"
  BaseFeature = -> Pad030
  Length = 8
  Length2 = 100
  Profile = -> Sketch097
  Type = 0
FEATURE [Sketcher::SketchObject] Sketch096
  MapMode = 5
  Placement = pos=(0,0,0) rot=(1,0,0;3.14159rad)
  Support = -> [Pad032]
  sketch-geometry (7):
    g0: LineSegment StartX=1.275 StartY=0.736122 StartZ=0 EndX=0 EndY=1.47224 EndZ=0
    g1: LineSegment StartX=0 StartY=1.47224 StartZ=0 EndX=-1.275 EndY=0.736122 EndZ=0
    g2: LineSegment StartX=-1.275 StartY=0.736122 StartZ=0 EndX=-1.275 EndY=-0.736122 EndZ=0
    g3: LineSegment StartX=-1.275 StartY=-0.736122 StartZ=0 EndX=1.34766e-11 EndY=-1.47224 EndZ=0
    g4: LineSegment StartX=1.34766e-11 StartY=-1.47224 StartZ=0 EndX=1.275 EndY=-0.736122 EndZ=0
    g5: LineSegment StartX=1.275 StartY=-0.736122 StartZ=0 EndX=1.275 EndY=0.736122 EndZ=0
    g6: Circle [constr] CenterX=0 CenterY=0 CenterZ=0 NormalX=0 NormalY=0 NormalZ=1 AngleXU=0 Radius=1.47224
  constraints (16):
    c: Coincident(g0,g1)
    c: Coincident(g1,g2)
    c: Coincident(g2,g3)
    c: Coincident(g3,g4)
    c: Coincident(g4,g5)
    c: Coincident(g5,g0)
    c: Equal(g0, g1-g5) x5
    c: PointOnObject(g0,g6)
    c: PointOnObject(g1,g6)
    c: PointOnObject(g2,g6)
    c: PointOnObject(g3,g6)
    c: PointOnObject(g4,g6)
    c: PointOnObject(g5,g6)
    c: Coincident(g6,g-1)
    c: PointOnObject(g0,g-2)
    c: DistanceX(g1,g0) = 2.55
FEATURE [PartDesign::Pocket] Pocket037  label="M3x8 Wrench154"
  BaseFeature = -> Pad032
  Length = 1.3
  Length2 = 100
  Profile = -> Sketch096
  Type = 0
FEATURE [PartDesign::Chamfer] Chamfer513  label="M3x8 Smooth005"
  Base = -> Pocket037 [Face11,Edge2,Edge24,Edge3]
  BaseFeature = -> Pocket037
  Size = 0.2
FEATURE [Sketcher::SketchObject] Sketch103
  MapMode = 5
  Support = -> [XY_Plane033]
  sketch-geometry (8):
    g0: LineSegment StartX=-35 StartY=70 StartZ=0 EndX=35 EndY=70 EndZ=0
    g1: LineSegment StartX=55 StartY=50 StartZ=0 EndX=55 EndY=25 EndZ=0
    g2: LineSegment StartX=30 StartY=0 StartZ=0 EndX=-30 EndY=0 EndZ=0
    g3: LineSegment StartX=-55 StartY=25 StartZ=0 EndX=-55 EndY=50 EndZ=0
    g4: ArcOfCircle CenterX=-35 CenterY=50 CenterZ=0 NormalX=0 NormalY=0 NormalZ=1 AngleXU=0 Radius=20 StartAngle=1.5708 EndAngle=3.14159
    g5: ArcOfCircle CenterX=35 CenterY=50 CenterZ=0 NormalX=0 NormalY=0 NormalZ=1 AngleXU=0 Radius=20 StartAngle=0 EndAngle=1.5708
    g6: ArcOfCircle CenterX=30 CenterY=25 CenterZ=0 NormalX=0 NormalY=0 NormalZ=1 AngleXU=0 Radius=25 StartAngle=4.71239 EndAngle=6.28319
    g7: ArcOfCircle CenterX=-30 CenterY=25 CenterZ=0 NormalX=0 NormalY=0 NormalZ=1 AngleXU=0 Radius=25 StartAngle=3.14159 EndAngle=4.71239
  constraints (19):
    c: Horizontal(g0)
    c: Horizontal(g2)
    c: Vertical(g1)
    c: Vertical(g3)
    c: Tangent(g3,g4) = 1.5708
    c: Tangent(g0,g4) = 1.5708
    c: Tangent(g0,g5) = 1.5708
    c: Tangent(g1,g5) = 1.5708
    c: Tangent(g1,g6) = 1.5708
    c: Tangent(g2,g6) = 1.5708
    c: Tangent(g2,g7) = 1.5708
    c: Tangent(g3,g7) = 1.5708
    c: Equal(g4,g5)
    c: Equal(g7,g6)
    c: Symmetric(g2,g2,g-1)
    c: Radius(g4) = 20
    c: Radius(g7) = 25
    c: DistanceY(g2,g0) = 70
    c: DistanceX(g3,g1) = 110
FEATURE [PartDesign::Pad] Pad1034  label="Baseplate043"
  Length = 5
  Length2 = 100
  Profile = -> Sketch103
  Type = 0
FEATURE [Sketcher::SketchObject] Sketch101
  MapMode = 5
  Support = -> [XY_Plane036]
  sketch-geometry (1):
    g0: Circle CenterX=0 CenterY=0 CenterZ=0 NormalX=0 NormalY=0 NormalZ=1 AngleXU=0 Radius=2.75
  constraints (2):
    c: Coincident(g0,g-1)
    c: Radius(g0) = 2.75
FEATURE [PartDesign::Pad] Pad1040  label="M3x8 Head004"
  Length = 3
  Length2 = 100
  Profile = -> Sketch101
  Type = 0
FEATURE [Sketcher::SketchObject] Sketch110
  MapMode = 5
  Support = -> [XY_Plane043]
  sketch-geometry (1):
    g0: Circle CenterX=0 CenterY=0 CenterZ=0 NormalX=0 NormalY=0 NormalZ=1 AngleXU=0 Radius=2.75
  constraints (2):
    c: Coincident(g0,g-1)
    c: Radius(g0) = 2.75
FEATURE [PartDesign::Pad] Pad041  label="M3x8 Head154"
  Length = 3
  Length2 = 100
  Profile = -> Sketch110
  Type = 0
FEATURE [Sketcher::SketchObject] Sketch099
  MapMode = 5
  Support = -> [XY_Plane951]
  sketch-geometry (1):
    g0: Circle CenterX=0 CenterY=0 CenterZ=0 NormalX=0 NormalY=0 NormalZ=1 AngleXU=0 Radius=2.75
  constraints (2):
    c: Coincident(g0,g-1)
    c: Radius(g0) = 2.75
FEATURE [PartDesign::Pad] Pad034  label="M3x8 Head155"
  Length = 3
  Length2 = 100
  Profile = -> Sketch099
  Type = 0
FEATURE [Sketcher::SketchObject] Sketch091
  MapMode = 5
  Placement = pos=(0,0,3) rot=(0,0,1;0rad)
  Support = -> [Pad034]
  sketch-geometry (1):
    g0: Circle CenterX=0 CenterY=0 CenterZ=0 NormalX=0 NormalY=0 NormalZ=1 AngleXU=0 Radius=1.5
  constraints (2):
    c: Coincident(g0,g-1)
    c: Radius(g0) = 1.5
FEATURE [PartDesign::Pad] Pad1038  label="M3x8 Thread005"
  BaseFeature = -> Pad034
  Length = 8
  Length2 = 100
  Profile = -> Sketch091
  Type = 0
FEATURE [Sketcher::SketchObject] Sketch100
  MapMode = 5
  Placement = pos=(0,0,0) rot=(1,0,0;3.14159rad)
  Support = -> [Pad1038]
  sketch-geometry (7):
    g0: LineSegment StartX=1.275 StartY=0.736122 StartZ=0 EndX=0 EndY=1.47224 EndZ=0
    g1: LineSegment StartX=0 StartY=1.47224 StartZ=0 EndX=-1.275 EndY=0.736122 EndZ=0
    g2: LineSegment StartX=-1.275 StartY=0.736122 StartZ=0 EndX=-1.275 EndY=-0.736122 EndZ=0
    g3: LineSegment StartX=-1.275 StartY=-0.736122 StartZ=0 EndX=1.34766e-11 EndY=-1.47224 EndZ=0
    g4: LineSegment StartX=1.34766e-11 StartY=-1.47224 StartZ=0 EndX=1.275 EndY=-0.736122 EndZ=0
    g5: LineSegment StartX=1.275 StartY=-0.736122 StartZ=0 EndX=1.275 EndY=0.736122 EndZ=0
    g6: Circle [constr] CenterX=0 CenterY=0 CenterZ=0 NormalX=0 NormalY=0 NormalZ=1 AngleXU=0 Radius=1.47224
  constraints (16):
    c: Coincident(g0,g1)
    c: Coincident(g1,g2)
    c: Coincident(g2,g3)
    c: Coincident(g3,g4)
    c: Coincident(g4,g5)
    c: Coincident(g5,g0)
    c: Equal(g0, g1-g5) x5
    c: PointOnObject(g0,g6)
    c: PointOnObject(g1,g6)
    c: PointOnObject(g2,g6)
    c: PointOnObject(g3,g6)
    c: PointOnObject(g4,g6)
    c: PointOnObject(g5,g6)
    c: Coincident(g6,g-1)
    c: PointOnObject(g0,g-2)
    c: DistanceX(g1,g0) = 2.55
FEATURE [PartDesign::Pocket] Pocket036  label="M3x8 Wrench006"
  BaseFeature = -> Pad1038
  Length = 1.3
  Length2 = 100
  Profile = -> Sketch100
  Type = 0
FEATURE [PartDesign::Chamfer] Chamfer510  label="M3x8 Smooth158"
  Base = -> Pocket036 [Face11,Edge2,Edge24,Edge3]
  BaseFeature = -> Pocket036
  Size = 0.2
FEATURE [Sketcher::SketchObject] Sketch105
  MapMode = 5
  Support = -> [XY_Plane947]
  sketch-geometry (4):
    g0: LineSegment StartX=-20 StartY=23.75 StartZ=0 EndX=20 EndY=23.75 EndZ=0
    g1: LineSegment StartX=20 StartY=23.75 StartZ=0 EndX=20 EndY=-23.75 EndZ=0
    g2: LineSegment StartX=20 StartY=-23.75 StartZ=0 EndX=-20 EndY=-23.75 EndZ=0
    g3: LineSegment StartX=-20 StartY=-23.75 StartZ=0 EndX=-20 EndY=23.75 EndZ=0
  constraints (10):
    c: Coincident(g0,g1)
    c: Coincident(g1,g2)
    c: Coincident(g2,g3)
    c: Coincident(g3,g0)
    c: Horizontal(g2)
    c: Vertical(g1)
    c: Symmetric(g0,g0,g-2)
    c: Symmetric(g0,g2,g-1)
    c: DistanceX(g0,g0) = 40
    c: DistanceY(g3,g3) = 47.5
FEATURE [PartDesign::Pad] Pad1039  label="Baseplate007"
  Length = 12
  Length2 = 100
  Profile = -> Sketch105
  Type = 0
FEATURE [Sketcher::SketchObject] Sketch102
  MapMode = 5
  Placement = pos=(0,0,3) rot=(0,0,1;0rad)
  Support = -> [Pad1040]
  sketch-geometry (1):
    g0: Circle CenterX=0 CenterY=0 CenterZ=0 NormalX=0 NormalY=0 NormalZ=1 AngleXU=0 Radius=1.5
  constraints (2):
    c: Coincident(g0,g-1)
    c: Radius(g0) = 1.5
FEATURE [PartDesign::Pad] Pad1035  label="M3x8 Thread004"
  BaseFeature = -> Pad1040
  Length = 8
  Length2 = 100
  Profile = -> Sketch102
  Type = 0
FEATURE [Sketcher::SketchObject] Sketch094
  MapMode = 5
  Placement = pos=(0,0,0) rot=(1,0,0;3.14159rad)
  Support = -> [Pad1035]
  sketch-geometry (7):
    g0: LineSegment StartX=1.275 StartY=0.736122 StartZ=0 EndX=0 EndY=1.47224 EndZ=0
    g1: LineSegment StartX=0 StartY=1.47224 StartZ=0 EndX=-1.275 EndY=0.736122 EndZ=0
    g2: LineSegment StartX=-1.275 StartY=0.736122 StartZ=0 EndX=-1.275 EndY=-0.736122 EndZ=0
    g3: LineSegment StartX=-1.275 StartY=-0.736122 StartZ=0 EndX=1.34766e-11 EndY=-1.47224 EndZ=0
    g4: LineSegment StartX=1.34766e-11 StartY=-1.47224 StartZ=0 EndX=1.275 EndY=-0.736122 EndZ=0
    g5: LineSegment StartX=1.275 StartY=-0.736122 StartZ=0 EndX=1.275 EndY=0.736122 EndZ=0
    g6: Circle [constr] CenterX=0 CenterY=0 CenterZ=0 NormalX=0 NormalY=0 NormalZ=1 AngleXU=0 Radius=1.47224
  constraints (16):
    c: Coincident(g0,g1)
    c: Coincident(g1,g2)
    c: Coincident(g2,g3)
    c: Coincident(g3,g4)
    c: Coincident(g4,g5)
    c: Coincident(g5,g0)
    c: Equal(g0, g1-g5) x5
    c: PointOnObject(g0,g6)
    c: PointOnObject(g1,g6)
    c: PointOnObject(g2,g6)
    c: PointOnObject(g3,g6)
    c: PointOnObject(g4,g6)
    c: PointOnObject(g5,g6)
    c: Coincident(g6,g-1)
    c: PointOnObject(g0,g-2)
    c: DistanceX(g1,g0) = 2.55
FEATURE [PartDesign::Pocket] Pocket032  label="M3x8 Wrench004"
  BaseFeature = -> Pad1035
  Length = 1.3
  Length2 = 100
  Profile = -> Sketch094
  Type = 0
FEATURE [PartDesign::Chamfer] Chamfer515  label="M3x8 Smooth006"
  Base = -> Pocket032 [Face11,Edge2,Edge24,Edge3]
  BaseFeature = -> Pocket032
  Size = 0.2
FEATURE [Sketcher::SketchObject] Sketch111
  MapMode = 5
  Placement = pos=(0,0,3) rot=(0,0,1;0rad)
  Support = -> [Pad041]
  sketch-geometry (1):
    g0: Circle CenterX=0 CenterY=0 CenterZ=0 NormalX=0 NormalY=0 NormalZ=1 AngleXU=0 Radius=1.5
  constraints (2):
    c: Coincident(g0,g-1)
    c: Radius(g0) = 1.5
FEATURE [PartDesign::Pad] Pad042  label="M3x8 Thread155"
  BaseFeature = -> Pad041
  Length = 8
  Length2 = 100
  Profile = -> Sketch111
  Type = 0
FEATURE [Sketcher::SketchObject] Sketch109
  MapMode = 5
  Placement = pos=(0,0,0) rot=(1,0,0;3.14159rad)
  Support = -> [Pad042]
  sketch-geometry (7):
    g0: LineSegment StartX=1.275 StartY=0.736122 StartZ=0 EndX=0 EndY=1.47224 EndZ=0
    g1: LineSegment StartX=0 StartY=1.47224 StartZ=0 EndX=-1.275 EndY=0.736122 EndZ=0
    g2: LineSegment StartX=-1.275 StartY=0.736122 StartZ=0 EndX=-1.275 EndY=-0.736122 EndZ=0
    g3: LineSegment StartX=-1.275 StartY=-0.736122 StartZ=0 EndX=1.34766e-11 EndY=-1.47224 EndZ=0
    g4: LineSegment StartX=1.34766e-11 StartY=-1.47224 StartZ=0 EndX=1.275 EndY=-0.736122 EndZ=0
    g5: LineSegment StartX=1.275 StartY=-0.736122 StartZ=0 EndX=1.275 EndY=0.736122 EndZ=0
    g6: Circle [constr] CenterX=0 CenterY=0 CenterZ=0 NormalX=0 NormalY=0 NormalZ=1 AngleXU=0 Radius=1.47224
  constraints (16):
    c: Coincident(g0,g1)
    c: Coincident(g1,g2)
    c: Coincident(g2,g3)
    c: Coincident(g3,g4)
    c: Coincident(g4,g5)
    c: Coincident(g5,g0)
    c: Equal(g0, g1-g5) x5
    c: PointOnObject(g0,g6)
    c: PointOnObject(g1,g6)
    c: PointOnObject(g2,g6)
    c: PointOnObject(g3,g6)
    c: PointOnObject(g4,g6)
    c: PointOnObject(g5,g6)
    c: Coincident(g6,g-1)
    c: PointOnObject(g0,g-2)
    c: DistanceX(g1,g0) = 2.55
FEATURE [PartDesign::Pocket] Pocket828  label="M3x8 Wrench155"
  BaseFeature = -> Pad042
  Length = 1.3
  Length2 = 100
  Profile = -> Sketch109
  Type = 0
FEATURE [Sketcher::SketchObject] Sketch2363
  MapMode = 5
  Support = -> [XY_Plane045]
  sketch-geometry (1):
    g0: Circle CenterX=0 CenterY=0 CenterZ=0 NormalX=0 NormalY=0 NormalZ=1 AngleXU=0 Radius=2.75
  constraints (2):
    c: Coincident(g0,g-1)
    c: Radius(g0) = 2.75
FEATURE [PartDesign::Pad] Pad045  label="M3x8 Head161"
  Length = 3
  Length2 = 100
  Profile = -> Sketch2363
  Type = 0
FEATURE [Sketcher::SketchObject] Sketch2364
  MapMode = 5
  Support = -> [XY_Plane046]
  sketch-geometry (1):
    g0: Circle CenterX=0 CenterY=0 CenterZ=0 NormalX=0 NormalY=0 NormalZ=1 AngleXU=0 Radius=2.75
  constraints (2):
    c: Coincident(g0,g-1)
    c: Radius(g0) = 2.75
FEATURE [PartDesign::Pad] Pad1046  label="M3x8 Head160"
  Length = 3
  Length2 = 100
  Profile = -> Sketch2364
  Type = 0
FEATURE [Sketcher::SketchObject] Sketch2365
  MapMode = 5
  Support = -> [XY_Plane048]
  sketch-geometry (1):
    g0: Circle CenterX=0 CenterY=0 CenterZ=0 NormalX=0 NormalY=0 NormalZ=1 AngleXU=0 Radius=2.75
  constraints (2):
    c: Coincident(g0,g-1)
    c: Radius(g0) = 2.75
FEATURE [PartDesign::Pad] Pad1045  label="M3x8 Head159"
  Length = 3
  Length2 = 100
  Profile = -> Sketch2365
  Type = 0
FEATURE [Sketcher::SketchObject] Sketch113
  MapMode = 5
  Support = -> [XY_Plane044]
  sketch-geometry (1):
    g0: Circle CenterX=0 CenterY=0 CenterZ=0 NormalX=0 NormalY=0 NormalZ=1 AngleXU=0 Radius=2.75
  constraints (2):
    c: Coincident(g0,g-1)
    c: Radius(g0) = 2.75
FEATURE [PartDesign::Pad] Pad043  label="M3x8 Head156"
  Length = 3
  Length2 = 100
  Profile = -> Sketch113
  Type = 0
FEATURE [Sketcher::SketchObject] Sketch2368
  MapMode = 5
  Support = -> [XY_Plane047]
  sketch-geometry (1):
    g0: Circle CenterX=0 CenterY=0 CenterZ=0 NormalX=0 NormalY=0 NormalZ=1 AngleXU=0 Radius=2.75
  constraints (2):
    c: Coincident(g0,g-1)
    c: Radius(g0) = 2.75
FEATURE [PartDesign::Pad] Pad1043  label="M3x8 Head158"
  Length = 3
  Length2 = 100
  Profile = -> Sketch2368
  Type = 0
FEATURE [Sketcher::SketchObject] Sketch2369
  MapMode = 5
  Placement = pos=(0,0,3) rot=(0,0,1;0rad)
  Support = -> [Pad1043]
  sketch-geometry (1):
    g0: Circle CenterX=0 CenterY=0 CenterZ=0 NormalX=0 NormalY=0 NormalZ=1 AngleXU=0 Radius=1.5
  constraints (2):
    c: Coincident(g0,g-1)
    c: Radius(g0) = 1.5
FEATURE [PartDesign::Pad] Pad1048  label="M3x8 Thread160"
  BaseFeature = -> Pad1043
  Length = 8
  Length2 = 100
  Profile = -> Sketch2369
  Type = 0
FEATURE [Sketcher::SketchObject] Sketch2367
  MapMode = 5
  Placement = pos=(0,0,0) rot=(1,0,0;3.14159rad)
  Support = -> [Pad1048]
  sketch-geometry (7):
    g0: LineSegment StartX=1.275 StartY=0.736122 StartZ=0 EndX=0 EndY=1.47224 EndZ=0
    g1: LineSegment StartX=0 StartY=1.47224 StartZ=0 EndX=-1.275 EndY=0.736122 EndZ=0
    g2: LineSegment StartX=-1.275 StartY=0.736122 StartZ=0 EndX=-1.275 EndY=-0.736122 EndZ=0
    g3: LineSegment StartX=-1.275 StartY=-0.736122 StartZ=0 EndX=1.34766e-11 EndY=-1.47224 EndZ=0
    g4: LineSegment StartX=1.34766e-11 StartY=-1.47224 StartZ=0 EndX=1.275 EndY=-0.736122 EndZ=0
    g5: LineSegment StartX=1.275 StartY=-0.736122 StartZ=0 EndX=1.275 EndY=0.736122 EndZ=0
    g6: Circle [constr] CenterX=0 CenterY=0 CenterZ=0 NormalX=0 NormalY=0 NormalZ=1 AngleXU=0 Radius=1.47224
  constraints (16):
    c: Coincident(g0,g1)
    c: Coincident(g1,g2)
    c: Coincident(g2,g3)
    c: Coincident(g3,g4)
    c: Coincident(g4,g5)
    c: Coincident(g5,g0)
    c: Equal(g0, g1-g5) x5
    c: PointOnObject(g0,g6)
    c: PointOnObject(g1,g6)
    c: PointOnObject(g2,g6)
    c: PointOnObject(g3,g6)
    c: PointOnObject(g4,g6)
    c: PointOnObject(g5,g6)
    c: Coincident(g6,g-1)
    c: PointOnObject(g0,g-2)
    c: DistanceX(g1,g0) = 2.55
FEATURE [PartDesign::Pocket] Pocket830  label="M3x8 Wrench157"
  BaseFeature = -> Pad1048
  Length = 1.3
  Length2 = 100
  Profile = -> Sketch2367
  Type = 0
FEATURE [PartDesign::Chamfer] Chamfer504  label="M3x8 Smooth154"
  Base = -> Pocket830 [Face11,Edge2,Edge24,Edge3]
  BaseFeature = -> Pocket830
  Size = 0.2
FEATURE [Sketcher::SketchObject] Sketch114
  MapMode = 5
  Placement = pos=(0,0,3) rot=(0,0,1;0rad)
  Support = -> [Pad043]
  sketch-geometry (1):
    g0: Circle CenterX=0 CenterY=0 CenterZ=0 NormalX=0 NormalY=0 NormalZ=1 AngleXU=0 Radius=1.5
  constraints (2):
    c: Coincident(g0,g-1)
    c: Radius(g0) = 1.5
FEATURE [PartDesign::Pad] Pad044  label="M3x8 Thread156"
  BaseFeature = -> Pad043
  Length = 8
  Length2 = 100
  Profile = -> Sketch114
  Type = 0
FEATURE [Sketcher::SketchObject] Sketch112
  MapMode = 5
  Placement = pos=(0,0,0) rot=(1,0,0;3.14159rad)
  Support = -> [Pad044]
  sketch-geometry (7):
    g0: LineSegment StartX=1.275 StartY=0.736122 StartZ=0 EndX=0 EndY=1.47224 EndZ=0
    g1: LineSegment StartX=0 StartY=1.47224 StartZ=0 EndX=-1.275 EndY=0.736122 EndZ=0
    g2: LineSegment StartX=-1.275 StartY=0.736122 StartZ=0 EndX=-1.275 EndY=-0.736122 EndZ=0
    g3: LineSegment StartX=-1.275 StartY=-0.736122 StartZ=0 EndX=1.34766e-11 EndY=-1.47224 EndZ=0
    g4: LineSegment StartX=1.34766e-11 StartY=-1.47224 StartZ=0 EndX=1.275 EndY=-0.736122 EndZ=0
    g5: LineSegment StartX=1.275 StartY=-0.736122 StartZ=0 EndX=1.275 EndY=0.736122 EndZ=0
    g6: Circle [constr] CenterX=0 CenterY=0 CenterZ=0 NormalX=0 NormalY=0 NormalZ=1 AngleXU=0 Radius=1.47224
  constraints (16):
    c: Coincident(g0,g1)
    c: Coincident(g1,g2)
    c: Coincident(g2,g3)
    c: Coincident(g3,g4)
    c: Coincident(g4,g5)
    c: Coincident(g5,g0)
    c: Equal(g0, g1-g5) x5
    c: PointOnObject(g0,g6)
    c: PointOnObject(g1,g6)
    c: PointOnObject(g2,g6)
    c: PointOnObject(g3,g6)
    c: PointOnObject(g4,g6)
    c: PointOnObject(g5,g6)
    c: Coincident(g6,g-1)
    c: PointOnObject(g0,g-2)
    c: DistanceX(g1,g0) = 2.55
FEATURE [PartDesign::Pocket] Pocket831  label="M3x8 Wrench158"
  BaseFeature = -> Pad044
  Length = 1.3
  Length2 = 100
  Profile = -> Sketch112
  Type = 0
FEATURE [Sketcher::SketchObject] Sketch2370
  MapMode = 5
  Placement = pos=(0,0,3) rot=(0,0,1;0rad)
  Support = -> [Pad045]
  sketch-geometry (1):
    g0: Circle CenterX=0 CenterY=0 CenterZ=0 NormalX=0 NormalY=0 NormalZ=1 AngleXU=0 Radius=1.5
  constraints (2):
    c: Coincident(g0,g-1)
    c: Radius(g0) = 1.5
FEATURE [PartDesign::Pad] Pad1047  label="M3x8 Thread158"
  BaseFeature = -> Pad045
  Length = 8
  Length2 = 100
  Profile = -> Sketch2370
  Type = 0
FEATURE [Sketcher::SketchObject] Sketch115
  MapMode = 5
  Placement = pos=(0,0,0) rot=(1,0,0;3.14159rad)
  Support = -> [Pad1047]
  sketch-geometry (7):
    g0: LineSegment StartX=1.275 StartY=0.736122 StartZ=0 EndX=0 EndY=1.47224 EndZ=0
    g1: LineSegment StartX=0 StartY=1.47224 StartZ=0 EndX=-1.275 EndY=0.736122 EndZ=0
    g2: LineSegment StartX=-1.275 StartY=0.736122 StartZ=0 EndX=-1.275 EndY=-0.736122 EndZ=0
    g3: LineSegment StartX=-1.275 StartY=-0.736122 StartZ=0 EndX=1.34766e-11 EndY=-1.47224 EndZ=0
    g4: LineSegment StartX=1.34766e-11 StartY=-1.47224 StartZ=0 EndX=1.275 EndY=-0.736122 EndZ=0
    g5: LineSegment StartX=1.275 StartY=-0.736122 StartZ=0 EndX=1.275 EndY=0.736122 EndZ=0
    g6: Circle [constr] CenterX=0 CenterY=0 CenterZ=0 NormalX=0 NormalY=0 NormalZ=1 AngleXU=0 Radius=1.47224
  constraints (16):
    c: Coincident(g0,g1)
    c: Coincident(g1,g2)
    c: Coincident(g2,g3)
    c: Coincident(g3,g4)
    c: Coincident(g4,g5)
    c: Coincident(g5,g0)
    c: Equal(g0, g1-g5) x5
    c: PointOnObject(g0,g6)
    c: PointOnObject(g1,g6)
    c: PointOnObject(g2,g6)
    c: PointOnObject(g3,g6)
    c: PointOnObject(g4,g6)
    c: PointOnObject(g5,g6)
    c: Coincident(g6,g-1)
    c: PointOnObject(g0,g-2)
    c: DistanceX(g1,g0) = 2.55
FEATURE [PartDesign::Pocket] Pocket829  label="M3x8 Wrench156"
  BaseFeature = -> Pad1047
  Length = 1.3
  Length2 = 100
  Profile = -> Sketch115
  Type = 0
FEATURE [PartDesign::Chamfer] Chamfer502  label="M3x8 Smooth152"
  Base = -> Pocket829 [Face11,Edge2,Edge24,Edge3]
  BaseFeature = -> Pocket829
  Size = 0.2
FEATURE [Sketcher::SketchObject] Sketch2372
  MapMode = 5
  Placement = pos=(0,0,3) rot=(0,0,1;0rad)
  Support = -> [Pad1046]
  sketch-geometry (1):
    g0: Circle CenterX=0 CenterY=0 CenterZ=0 NormalX=0 NormalY=0 NormalZ=1 AngleXU=0 Radius=1.5
  constraints (2):
    c: Coincident(g0,g-1)
    c: Radius(g0) = 1.5
FEATURE [PartDesign::Pad] Pad1044  label="M3x8 Thread157"
  BaseFeature = -> Pad1046
  Length = 8
  Length2 = 100
  Profile = -> Sketch2372
  Type = 0
FEATURE [Sketcher::SketchObject] Sketch2371
  MapMode = 5
  Placement = pos=(0,0,0) rot=(1,0,0;3.14159rad)
  Support = -> [Pad1044]
  sketch-geometry (7):
    g0: LineSegment StartX=1.275 StartY=0.736122 StartZ=0 EndX=0 EndY=1.47224 EndZ=0
    g1: LineSegment StartX=0 StartY=1.47224 StartZ=0 EndX=-1.275 EndY=0.736122 EndZ=0
    g2: LineSegment StartX=-1.275 StartY=0.736122 StartZ=0 EndX=-1.275 EndY=-0.736122 EndZ=0
    g3: LineSegment StartX=-1.275 StartY=-0.736122 StartZ=0 EndX=1.34766e-11 EndY=-1.47224 EndZ=0
    g4: LineSegment StartX=1.34766e-11 StartY=-1.47224 StartZ=0 EndX=1.275 EndY=-0.736122 EndZ=0
    g5: LineSegment StartX=1.275 StartY=-0.736122 StartZ=0 EndX=1.275 EndY=0.736122 EndZ=0
    g6: Circle [constr] CenterX=0 CenterY=0 CenterZ=0 NormalX=0 NormalY=0 NormalZ=1 AngleXU=0 Radius=1.47224
  constraints (16):
    c: Coincident(g0,g1)
    c: Coincident(g1,g2)
    c: Coincident(g2,g3)
    c: Coincident(g3,g4)
    c: Coincident(g4,g5)
    c: Coincident(g5,g0)
    c: Equal(g0, g1-g5) x5
    c: PointOnObject(g0,g6)
    c: PointOnObject(g1,g6)
    c: PointOnObject(g2,g6)
    c: PointOnObject(g3,g6)
    c: PointOnObject(g4,g6)
    c: PointOnObject(g5,g6)
    c: Coincident(g6,g-1)
    c: PointOnObject(g0,g-2)
    c: DistanceX(g1,g0) = 2.55
FEATURE [PartDesign::Pocket] Pocket834  label="M3x8 Wrench161"
  BaseFeature = -> Pad1044
  Length = 1.3
  Length2 = 100
  Profile = -> Sketch2371
  Type = 0
FEATURE [PartDesign::Chamfer] Chamfer506  label="M3x8 Smooth156"
  Base = -> Pocket834 [Face11,Edge2,Edge24,Edge3]
  BaseFeature = -> Pocket834
  Size = 0.2
FEATURE [Sketcher::SketchObject] Sketch2374
  MapMode = 5
  Placement = pos=(0,0,3) rot=(0,0,1;0rad)
  Support = -> [Pad1045]
  sketch-geometry (1):
    g0: Circle CenterX=0 CenterY=0 CenterZ=0 NormalX=0 NormalY=0 NormalZ=1 AngleXU=0 Radius=1.5
  constraints (2):
    c: Coincident(g0,g-1)
    c: Radius(g0) = 1.5
FEATURE [PartDesign::Pad] Pad1049  label="M3x8 Thread161"
  BaseFeature = -> Pad1045
  Length = 8
  Length2 = 100
  Profile = -> Sketch2374
  Type = 0
FEATURE [Sketcher::SketchObject] Sketch2373
  MapMode = 5
  Placement = pos=(0,0,0) rot=(1,0,0;3.14159rad)
  Support = -> [Pad1049]
  sketch-geometry (7):
    g0: LineSegment StartX=1.275 StartY=0.736122 StartZ=0 EndX=0 EndY=1.47224 EndZ=0
    g1: LineSegment StartX=0 StartY=1.47224 StartZ=0 EndX=-1.275 EndY=0.736122 EndZ=0
    g2: LineSegment StartX=-1.275 StartY=0.736122 StartZ=0 EndX=-1.275 EndY=-0.736122 EndZ=0
    g3: LineSegment StartX=-1.275 StartY=-0.736122 StartZ=0 EndX=1.34766e-11 EndY=-1.47224 EndZ=0
    g4: LineSegment StartX=1.34766e-11 StartY=-1.47224 StartZ=0 EndX=1.275 EndY=-0.736122 EndZ=0
    g5: LineSegment StartX=1.275 StartY=-0.736122 StartZ=0 EndX=1.275 EndY=0.736122 EndZ=0
    g6: Circle [constr] CenterX=0 CenterY=0 CenterZ=0 NormalX=0 NormalY=0 NormalZ=1 AngleXU=0 Radius=1.47224
  constraints (16):
    c: Coincident(g0,g1)
    c: Coincident(g1,g2)
    c: Coincident(g2,g3)
    c: Coincident(g3,g4)
    c: Coincident(g4,g5)
    c: Coincident(g5,g0)
    c: Equal(g0, g1-g5) x5
    c: PointOnObject(g0,g6)
    c: PointOnObject(g1,g6)
    c: PointOnObject(g2,g6)
    c: PointOnObject(g3,g6)
    c: PointOnObject(g4,g6)
    c: PointOnObject(g5,g6)
    c: Coincident(g6,g-1)
    c: PointOnObject(g0,g-2)
    c: DistanceX(g1,g0) = 2.55
FEATURE [PartDesign::Pocket] Pocket832  label="M3x8 Wrench159"
  BaseFeature = -> Pad1049
  Length = 1.3
  Length2 = 100
  Profile = -> Sketch2373
  Type = 0
FEATURE [PartDesign::Chamfer] Chamfer505  label="M3x8 Smooth155"
  Base = -> Pocket832 [Face11,Edge2,Edge24,Edge3]
  BaseFeature = -> Pocket832
  Size = 0.2
FEATURE [Sketcher::SketchObject] Sketch2376
  MapMode = 5
  Support = -> [XY_Plane049]
  sketch-geometry (1):
    g0: Circle CenterX=0 CenterY=0 CenterZ=0 NormalX=0 NormalY=0 NormalZ=1 AngleXU=0 Radius=2.75
  constraints (2):
    c: Coincident(g0,g-1)
    c: Radius(g0) = 2.75
FEATURE [PartDesign::Pad] Pad1042  label="M3x8 Head157"
  Length = 3
  Length2 = 100
  Profile = -> Sketch2376
  Type = 0
FEATURE [Sketcher::SketchObject] Sketch2377
  MapMode = 5
  Support = -> [XY_Plane050]
  sketch-geometry (1):
    g0: Circle CenterX=0 CenterY=0 CenterZ=0 NormalX=0 NormalY=0 NormalZ=1 AngleXU=0 Radius=2.75
  constraints (2):
    c: Coincident(g0,g-1)
    c: Radius(g0) = 2.75
FEATURE [PartDesign::Pad] Pad055  label="M3x8 Head162"
  Length = 3
  Length2 = 100
  Profile = -> Sketch2377
  Type = 0
FEATURE [Sketcher::SketchObject] Sketch2375
  MapMode = 5
  Placement = pos=(0,0,3) rot=(0,0,1;0rad)
  Support = -> [Pad055]
  sketch-geometry (1):
    g0: Circle CenterX=0 CenterY=0 CenterZ=0 NormalX=0 NormalY=0 NormalZ=1 AngleXU=0 Radius=1.5
  constraints (2):
    c: Coincident(g0,g-1)
    c: Radius(g0) = 1.5
FEATURE [PartDesign::Pad] Pad056  label="M3x8 Thread162"
  BaseFeature = -> Pad055
  Length = 8
  Length2 = 100
  Profile = -> Sketch2375
  Type = 0
FEATURE [Sketcher::SketchObject] Sketch2378
  MapMode = 5
  Placement = pos=(0,0,3) rot=(0,0,1;0rad)
  Support = -> [Pad1042]
  sketch-geometry (1):
    g0: Circle CenterX=0 CenterY=0 CenterZ=0 NormalX=0 NormalY=0 NormalZ=1 AngleXU=0 Radius=1.5
  constraints (2):
    c: Coincident(g0,g-1)
    c: Radius(g0) = 1.5
FEATURE [PartDesign::Pad] Pad054  label="M3x8 Thread159"
  BaseFeature = -> Pad1042
  Length = 8
  Length2 = 100
  Profile = -> Sketch2378
  Type = 0
FEATURE [Sketcher::SketchObject] Sketch2366
  MapMode = 5
  Placement = pos=(0,0,0) rot=(1,0,0;3.14159rad)
  Support = -> [Pad054]
  sketch-geometry (7):
    g0: LineSegment StartX=1.275 StartY=0.736122 StartZ=0 EndX=0 EndY=1.47224 EndZ=0
    g1: LineSegment StartX=0 StartY=1.47224 StartZ=0 EndX=-1.275 EndY=0.736122 EndZ=0
    g2: LineSegment StartX=-1.275 StartY=0.736122 StartZ=0 EndX=-1.275 EndY=-0.736122 EndZ=0
    g3: LineSegment StartX=-1.275 StartY=-0.736122 StartZ=0 EndX=1.34766e-11 EndY=-1.47224 EndZ=0
    g4: LineSegment StartX=1.34766e-11 StartY=-1.47224 StartZ=0 EndX=1.275 EndY=-0.736122 EndZ=0
    g5: LineSegment StartX=1.275 StartY=-0.736122 StartZ=0 EndX=1.275 EndY=0.736122 EndZ=0
    g6: Circle [constr] CenterX=0 CenterY=0 CenterZ=0 NormalX=0 NormalY=0 NormalZ=1 AngleXU=0 Radius=1.47224
  constraints (16):
    c: Coincident(g0,g1)
    c: Coincident(g1,g2)
    c: Coincident(g2,g3)
    c: Coincident(g3,g4)
    c: Coincident(g4,g5)
    c: Coincident(g5,g0)
    c: Equal(g0, g1-g5) x5
    c: PointOnObject(g0,g6)
    c: PointOnObject(g1,g6)
    c: PointOnObject(g2,g6)
    c: PointOnObject(g3,g6)
    c: PointOnObject(g4,g6)
    c: PointOnObject(g5,g6)
    c: Coincident(g6,g-1)
    c: PointOnObject(g0,g-2)
    c: DistanceX(g1,g0) = 2.55
FEATURE [PartDesign::Pocket] Pocket833  label="M3x8 Wrench160"
  BaseFeature = -> Pad054
  Length = 1.3
  Length2 = 100
  Profile = -> Sketch2366
  Type = 0
FEATURE [Sketcher::SketchObject] Sketch2379
  MapMode = 5
  Placement = pos=(0,0,0) rot=(1,0,0;3.14159rad)
  Support = -> [Pad056]
  sketch-geometry (7):
    g0: LineSegment StartX=1.275 StartY=0.736122 StartZ=0 EndX=0 EndY=1.47224 EndZ=0
    g1: LineSegment StartX=0 StartY=1.47224 StartZ=0 EndX=-1.275 EndY=0.736122 EndZ=0
    g2: LineSegment StartX=-1.275 StartY=0.736122 StartZ=0 EndX=-1.275 EndY=-0.736122 EndZ=0
    g3: LineSegment StartX=-1.275 StartY=-0.736122 StartZ=0 EndX=1.34766e-11 EndY=-1.47224 EndZ=0
    g4: LineSegment StartX=1.34766e-11 StartY=-1.47224 StartZ=0 EndX=1.275 EndY=-0.736122 EndZ=0
    g5: LineSegment StartX=1.275 StartY=-0.736122 StartZ=0 EndX=1.275 EndY=0.736122 EndZ=0
    g6: Circle [constr] CenterX=0 CenterY=0 CenterZ=0 NormalX=0 NormalY=0 NormalZ=1 AngleXU=0 Radius=1.47224
  constraints (16):
    c: Coincident(g0,g1)
    c: Coincident(g1,g2)
    c: Coincident(g2,g3)
    c: Coincident(g3,g4)
    c: Coincident(g4,g5)
    c: Coincident(g5,g0)
    c: Equal(g0, g1-g5) x5
    c: PointOnObject(g0,g6)
    c: PointOnObject(g1,g6)
    c: PointOnObject(g2,g6)
    c: PointOnObject(g3,g6)
    c: PointOnObject(g4,g6)
    c: PointOnObject(g5,g6)
    c: Coincident(g6,g-1)
    c: PointOnObject(g0,g-2)
    c: DistanceX(g1,g0) = 2.55
FEATURE [PartDesign::Pocket] Pocket840  label="M3x8 Wrench162"
  BaseFeature = -> Pad056
  Length = 1.3
  Length2 = 100
  Profile = -> Sketch2379
  Type = 0
FEATURE [PartDesign::Chamfer] Chamfer503  label="M3x8 Smooth153"
  Base = -> Pocket840 [Face11,Edge2,Edge24,Edge3]
  BaseFeature = -> Pocket840
  Size = 0.2
FEATURE [PartDesign::Chamfer] Chamfer519  label="M3x8 Smooth159"
  Base = -> Pocket828 [Face11,Edge2,Edge24,Edge3]
  BaseFeature = -> Pocket828
  Size = 0.2
FEATURE [PartDesign::Body] Body656  label="M3 Nut103"
  Group = -> [Sketch020,Pad1031,Sketch021,Groove212,Chamfer509]
  Origin = -> Origin969
  Placement = pos=(-5,-35.75,6) rot=(1,0,0;1.5708rad)
  Tip = -> Chamfer509
FEATURE [PartDesign::Body] Body657  label="M3 Nut104"
  Group = -> [Sketch022,Pad1033,Sketch064,Groove213,Chamfer012]
  Origin = -> Origin970
  Placement = pos=(5,-35.75,6) rot=(1,0,0;1.5708rad)
  Tip = -> Chamfer012
FEATURE [PartDesign::Body] Body658  label="Inner_Shoulder"
  Group = -> [Sketch048,Pad020,Sketch058,Pocket022,Sketch049,Pocket024,Sketch057,Pocket023,Fillet256,Sketch053,Pocket021,Chamfer014,Sketch050,Pocket026,Sketch059,Pocket025]
  Origin = -> Origin961
  Placement = pos=(0,0,0) rot=(1,0,0;1.5708rad)
  Tip = -> Pocket025
FEATURE [PartDesign::Body] Body659  label="Bottom_Shoulder"
  Group = -> [Sketch060,Pad1032,Sketch062,Pocket818,Sketch054,Pocket819,Sketch055,Pocket817,Sketch051,Pocket820,Sketch056,Pocket821,Fillet257,Fillet012]
  Origin = -> Origin966
  Placement = pos=(0,-55,0) rot=(0,0,1;0rad)
  Tip = -> Fillet012
FEATURE [PartDesign::Body] Body014  label="M3x121"
  Group = -> [Sketch042,Pad016,Sketch047,Pad018,Sketch038,Pocket020,Chamfer011]
  Origin = -> Origin964
  Placement = pos=(-15,-1.4e-14,64) rot=(1,0,0;1.5708rad)
  Tip = -> Chamfer011
FEATURE [PartDesign::Body] Body660  label="M3 Nut105"
  Group = -> [Sketch067,Pad006,Sketch068,Groove214,Chamfer004]
  Origin = -> Origin963
  Placement = pos=(15,-110.75,66) rot=(1,0,0;1.5708rad)
  Tip = -> Chamfer004
FEATURE [PartDesign::Body] Body661  label="Top_Shoulder"
  Group = -> [Sketch052,Pad1030,Sketch2361,Pocket027,Sketch2359,Pocket816,Sketch061,Pocket028,Sketch2360,Pocket030,Sketch065,Pocket029,Fillet014,Fillet013,Sketch2362,Pocket016]
  Origin = -> Origin965
  Placement = pos=(0,-130,60) rot=(0,0,1;0rad)
  Tip = -> Pocket016
FEATURE [PartDesign::Body] Body019  label="M3 Nut106"
  Group = -> [Sketch066,Pad1029,Sketch063,Groove211,Chamfer508]
  Origin = -> Origin967
  Placement = pos=(-15,-110.75,66) rot=(1,0,0;1.5708rad)
  Tip = -> Chamfer508
FEATURE [PartDesign::Body] Body662  label="M3x122"
  Group = -> [Sketch039,Pad015,Sketch036,Pad013,Sketch045,Pocket017,Chamfer009]
  Origin = -> Origin949
  Placement = pos=(5,-1e-15,6) rot=(1,0,0;1.5708rad)
  Tip = -> Chamfer009
FEATURE [PartDesign::Body] Body663  label="M3x123"
  Group = -> [Sketch037,Pad014,Sketch043,Pad019,Sketch041,Pocket019,Chamfer010]
  Origin = -> Origin947
  Placement = pos=(15,-1.4e-14,64) rot=(1,0,0;1.5708rad)
  Tip = -> Chamfer010
FEATURE [PartDesign::Body] Body669  label="M3x124"
  Group = -> [Sketch044,Pad017,Sketch046,Pad012,Sketch040,Pocket018,Chamfer013]
  Origin = -> Origin968
  Placement = pos=(-5,-1e-15,6) rot=(1,0,0;1.5708rad)
  Tip = -> Chamfer013
FEATURE [PartDesign::Body] Body032  label="M3x125"
  Group = -> [Sketch101,Pad1040,Sketch102,Pad1035,Sketch094,Pocket032,Chamfer515]
  Origin = -> Origin951
  Placement = pos=(-5,-1e-15,6) rot=(1,0,0;1.5708rad)
  Tip = -> Chamfer515
FEATURE [PartDesign::Body] Body035  label="M3x126"
  Group = -> [Sketch2363,Pad045,Sketch2370,Pad1047,Sketch115,Pocket829,Chamfer502]
  Origin = -> Origin045
  Placement = pos=(106.75,2e-15,7.5) rot=(-1,0,0;1.5708rad)
  Tip = -> Chamfer502
FEATURE [PartDesign::Body] Body026  label="M3x127"
  Group = -> [Sketch099,Pad034,Sketch091,Pad1038,Sketch100,Pocket036,Chamfer510]
  Origin = -> Origin036
  Placement = pos=(-15,-1.4e-14,64) rot=(1,0,0;1.5708rad)
  Tip = -> Chamfer510
FEATURE [PartDesign::Body] Body030  label="M3x128"
  Group = -> [Sketch098,Pad031,Sketch089,Pad033,Sketch090,Pocket033,Chamfer516]
  Origin = -> Origin031
  Placement = pos=(5,-1e-15,6) rot=(1,0,0;1.5708rad)
  Tip = -> Chamfer516
FEATURE [PartDesign::Body] Body031  label="M3x129"
  Group = -> [Sketch088,Pad030,Sketch097,Pad032,Sketch096,Pocket037,Chamfer513]
  Origin = -> Origin952
  Placement = pos=(15,-1.4e-14,64) rot=(1,0,0;1.5708rad)
  Tip = -> Chamfer513
FEATURE [PartDesign::Body] Body033  label="M3x130"
  Group = -> [Sketch110,Pad041,Sketch111,Pad042,Sketch109,Pocket828,Chamfer519]
  Origin = -> Origin043
  Placement = pos=(3.25,2e-15,7.5) rot=(-1,0,0;1.5708rad)
  Tip = -> Chamfer519
FEATURE [Sketcher::SketchObject] Sketch025
  MapMode = 5
  Support = -> [XY_Plane009]
  sketch-geometry (4):
    g0: LineSegment StartX=-12.5 StartY=75 StartZ=0 EndX=12.5 EndY=75 EndZ=0
    g1: LineSegment StartX=12.5 StartY=75 StartZ=0 EndX=12.5 EndY=-75 EndZ=0
    g2: LineSegment StartX=12.5 StartY=-75 StartZ=0 EndX=-12.5 EndY=-75 EndZ=0
    g3: LineSegment StartX=-12.5 StartY=-75 StartZ=0 EndX=-12.5 EndY=75 EndZ=0
  constraints (10):
    c: Coincident(g0,g1)
    c: Coincident(g1,g2)
    c: Coincident(g2,g3)
    c: Coincident(g3,g0)
    c: Horizontal(g2)
    c: Vertical(g3)
    c: Symmetric(g0,g0,g-2)
    c: Symmetric(g1,g0,g-1)
    c: DistanceX(g0,g0) = 25
    c: DistanceY(g1,g0) = 150
FEATURE [PartDesign::Pad] Pad007  label="Baseplate045"
  Length = 6.5
  Length2 = 100
  Profile = -> Sketch025
  Type = 0
FEATURE [Sketcher::SketchObject] Sketch030
  MapMode = 5
  Support = -> [XY_Plane954]
  sketch-geometry (8):
    g0: LineSegment StartX=0 StartY=3.17543 StartZ=0 EndX=-2.75 EndY=1.58771 EndZ=0
    g1: LineSegment StartX=-2.75 StartY=1.58771 StartZ=0 EndX=-2.75 EndY=-1.58771 EndZ=0
    g2: LineSegment StartX=-2.75 StartY=-1.58771 StartZ=0 EndX=0 EndY=-3.17543 EndZ=0
    g3: LineSegment StartX=0 StartY=-3.17543 StartZ=0 EndX=2.75 EndY=-1.58771 EndZ=0
    g4: LineSegment StartX=2.75 StartY=-1.58771 StartZ=0 EndX=2.75 EndY=1.58771 EndZ=0
    g5: LineSegment StartX=2.75 StartY=1.58771 StartZ=0 EndX=0 EndY=3.17543 EndZ=0
    g6: Circle [constr] CenterX=0 CenterY=0 CenterZ=0 NormalX=0 NormalY=0 NormalZ=1 AngleXU=0 Radius=3.17543
    g7: Circle CenterX=0 CenterY=0 CenterZ=0 NormalX=0 NormalY=0 NormalZ=1 AngleXU=0 Radius=1.5
  constraints (18):
    c: Coincident(g0,g1)
    c: Coincident(g1,g2)
    c: Coincident(g2,g3)
    c: Coincident(g3,g4)
    c: Coincident(g4,g5)
    c: Coincident(g5,g0)
    c: Equal(g0, g1-g5) x5
    c: PointOnObject(g0,g6)
    c: PointOnObject(g1,g6)
    c: PointOnObject(g2,g6)
    c: PointOnObject(g3,g6)
    c: PointOnObject(g4,g6)
    c: PointOnObject(g5,g6)
    c: Coincident(g6,g-1)
    c: PointOnObject(g5,g-2)
    c: DistanceX(g0,g4) = 5.5
    c: Coincident(g7,g-1)
    c: Radius(g7) = 1.5
FEATURE [PartDesign::Pad] Pad1050  label="M3 Nut Primitive004"
  Length = 1.2
  Length2 = 1.2
  Profile = -> Sketch030
  Type = 4
FEATURE [Sketcher::SketchObject] Sketch024
  MapMode = 5
  Placement = pos=(0,-75,0) rot=(1,0,0;1.5708rad)
  Support = -> [Pad007]
  sketch-geometry (2):
    g0: Circle CenterX=-7.5 CenterY=3.25 CenterZ=0 NormalX=0 NormalY=0 NormalZ=1 AngleXU=0 Radius=1.6
    g1: Circle CenterX=7.5 CenterY=3.25 CenterZ=0 NormalX=0 NormalY=0 NormalZ=1 AngleXU=0 Radius=1.6
  constraints (5):
    c: Symmetric(g0,g1,g-2)
    c: DistanceY(g-1,g0) = 3.25
    c: Equal(g0,g1)
    c: Radius(g1) = 1.6
    c: DistanceX(g0,g1) = 15
FEATURE [PartDesign::Pocket] Pocket015  label="Screwholes Front001"
  BaseFeature = -> Pad007
  Length = 10
  Length2 = 100
  Profile = -> Sketch024
  Type = 0
FEATURE [Sketcher::SketchObject] Sketch023
  MapMode = 5
  Placement = pos=(0,75,0) rot=(0,0.707107,0.707107;3.14159rad)
  Support = -> [Pocket015]
  sketch-geometry (2):
    g0: Circle CenterX=-7.5 CenterY=3.25 CenterZ=0 NormalX=0 NormalY=0 NormalZ=1 AngleXU=0 Radius=1.6
    g1: Circle CenterX=7.5 CenterY=3.25 CenterZ=0 NormalX=0 NormalY=0 NormalZ=1 AngleXU=0 Radius=1.6
  constraints (5):
    c: Symmetric(g1,g0,g-2)
    c: Equal(g0,g1)
    c: DistanceY(g-1,g0) = 3.25
    c: Radius(g1) = 1.6
    c: DistanceX(g0,g1) = 15
FEATURE [PartDesign::Pocket] Pocket838  label="Screwholes Rear001"
  BaseFeature = -> Pocket015
  Length = 10
  Length2 = 100
  Profile = -> Sketch023
  Type = 0
FEATURE [Sketcher::SketchObject] Sketch027
  MapMode = 5
  Placement = pos=(0,0,6.5) rot=(0,0,1;0rad)
  Support = -> [Pocket838]
  sketch-geometry (16):
    g0: LineSegment StartX=-10.4 StartY=72 StartZ=0 EndX=-4.6 EndY=72 EndZ=0
    g1: LineSegment StartX=-4.6 StartY=72 StartZ=0 EndX=-4.6 EndY=69 EndZ=0
    g2: LineSegment StartX=-4.6 StartY=69 StartZ=0 EndX=-10.4 EndY=69 EndZ=0
    g3: LineSegment StartX=-10.4 StartY=69 StartZ=0 EndX=-10.4 EndY=72 EndZ=0
    g4: LineSegment StartX=4.6 StartY=72 StartZ=0 EndX=10.4 EndY=72 EndZ=0
    g5: LineSegment StartX=10.4 StartY=72 StartZ=0 EndX=10.4 EndY=69 EndZ=0
    g6: LineSegment StartX=10.4 StartY=69 StartZ=0 EndX=4.6 EndY=69 EndZ=0
    g7: LineSegment StartX=4.6 StartY=69 StartZ=0 EndX=4.6 EndY=72 EndZ=0
    g8: LineSegment StartX=-10.4 StartY=-69 StartZ=0 EndX=-4.6 EndY=-69 EndZ=0
    g9: LineSegment StartX=-4.6 StartY=-69 StartZ=0 EndX=-4.6 EndY=-72 EndZ=0
    g10: LineSegment StartX=-4.6 StartY=-72 StartZ=0 EndX=-10.4 EndY=-72 EndZ=0
    g11: LineSegment StartX=-10.4 StartY=-72 StartZ=0 EndX=-10.4 EndY=-69 EndZ=0
    g12: LineSegment StartX=4.6 StartY=-69 StartZ=0 EndX=10.4 EndY=-69 EndZ=0
    g13: LineSegment StartX=10.4 StartY=-69 StartZ=0 EndX=10.4 EndY=-72 EndZ=0
    g14: LineSegment StartX=10.4 StartY=-72 StartZ=0 EndX=4.6 EndY=-72 EndZ=0
    g15: LineSegment StartX=4.6 StartY=-72 StartZ=0 EndX=4.6 EndY=-69 EndZ=0
  constraints (45):
    c: Coincident(g0,g1)
    c: Coincident(g1,g2)
    c: Coincident(g2,g3)
    c: Coincident(g3,g0)
    c: Horizontal(g0)
    c: Horizontal(g2)
    c: Vertical(g1)
    c: Vertical(g3)
    c: Coincident(g4,g5)
    c: Coincident(g5,g6)
    c: Coincident(g6,g7)
    c: Coincident(g7,g4)
    c: Horizontal(g4)
    c: Horizontal(g6)
    c: Vertical(g5)
    c: Vertical(g7)
    c: Coincident(g8,g9)
    c: Coincident(g9,g10)
    c: Coincident(g10,g11)
    c: Coincident(g11,g8)
    c: Horizontal(g8)
    c: Horizontal(g10)
    c: Vertical(g9)
    c: Vertical(g11)
    c: Coincident(g12,g13)
    c: Coincident(g13,g14)
    c: Coincident(g14,g15)
    c: Coincident(g15,g12)
    c: Horizontal(g12)
    c: Horizontal(g14)
    c: Vertical(g13)
    c: Vertical(g15)
    c: Symmetric(g9,g14,g-2)
    c: Symmetric(g0,g4,g-2)
    c: Equal(g3,g5)
    c: Equal(g5,g13)
    c: Equal(g13,g11)
    c: Equal(g10,g14)
    c: Equal(g14,g0)
    c: Equal(g0,g4)
    c: DistanceX(g4,g4) = 5.8
    c: DistanceY(g3,g3) = 3
    c: DistanceY(g-1,g4) = 72
    c: DistanceX(g0,g4) = 9.2
    c: Symmetric(g12,g5,g-1)
FEATURE [PartDesign::Pocket] Pocket836  label="Nutholes Front and Rear001"
  BaseFeature = -> Pocket838
  Length = 6.5
  Length2 = 100
  Profile = -> Sketch027
  Type = 0
FEATURE [PartDesign::Fillet] Fillet006  label="Smooth Baseplate Corners002"
  Base = -> Pocket836 [Edge7,Edge46,Edge4,Edge1]
  BaseFeature = -> Pocket836
  Radius = 0.4
FEATURE [PartDesign::Fillet] Fillet007  label="Smooth Nuthole Corners001"
  Base = -> Fillet006 [Edge77,Edge82,Edge71,Edge65,Edge72,Edge66,Edge78,Edge83,Edge84,Edge79,Edge68,Edge74,Edge75,Edge69,Edge80,Edge85]
  BaseFeature = -> Fillet006
  Radius = 0.2
FEATURE [Sketcher::SketchObject] Sketch026
  MapMode = 5
  Placement = pos=(0,0,6.5) rot=(0,0,1;0rad)
  Support = -> [Fillet007]
  sketch-geometry (8):
    g0: LineSegment StartX=-10 StartY=-60 StartZ=0 EndX=-10 EndY=60 EndZ=0
    g1: LineSegment StartX=-10 StartY=60 StartZ=0 EndX=-4.5 EndY=60 EndZ=0
    g2: LineSegment StartX=-4.5 StartY=60 StartZ=0 EndX=-4.5 EndY=50 EndZ=0
    g3: LineSegment StartX=-4.5 StartY=50 StartZ=0 EndX=10 EndY=50 EndZ=0
    g4: LineSegment StartX=10 StartY=50 StartZ=0 EndX=10 EndY=-50 EndZ=0
    g5: LineSegment StartX=10 StartY=-50 StartZ=0 EndX=-4.5 EndY=-50 EndZ=0
    g6: LineSegment StartX=-4.5 StartY=-50 StartZ=0 EndX=-4.5 EndY=-60 EndZ=0
    g7: LineSegment StartX=-4.5 StartY=-60 StartZ=0 EndX=-10 EndY=-60 EndZ=0
  constraints (22):
    c: Coincident(g0,g1)
    c: Horizontal(g1)
    c: Coincident(g1,g2)
    c: Vertical(g2)
    c: Coincident(g2,g3)
    c: Horizontal(g3)
    c: Coincident(g3,g4)
    c: Coincident(g4,g5)
    c: Coincident(g5,g6)
    c: Vertical(g6)
    c: Coincident(g6,g7)
    c: Coincident(g7,g0)
    c: Equal(g2,g6)
    c: Equal(g3,g5)
    c: Symmetric(g2,g5,g-1)
    c: Symmetric(g3,g4,g-1)
    c: Symmetric(g0,g0,g-1)
    c: DistanceY(g0,g0) = 120
    c: DistanceX(g1,g1) = 5.5
    c: DistanceX(g1,g-1) = 4.5
    c: DistanceX(g-1,g3) = 10
    c: DistanceY(g2,g2) = 10
FEATURE [PartDesign::Pocket] Pocket835  label="Circuitboard Mount001"
  BaseFeature = -> Fillet007
  Length = 5
  Length2 = 100
  Profile = -> Sketch026
  Type = 0
FEATURE [PartDesign::Fillet] Fillet258  label="Smooth Circuitboard Mount Top Corners001"
  Base = -> Pocket835 [Edge158,Edge160,Edge164,Edge162]
  BaseFeature = -> Pocket835
  Radius = 1
FEATURE [PartDesign::Fillet] Fillet008  label="Smooth Circuitboard Mount Bottom Corners001"
  Base = -> Fillet258 [Edge54,Edge58,Edge66,Edge62]
  BaseFeature = -> Fillet258
  Radius = 0.2
FEATURE [PartDesign::Body] Body666  label="Chassis_Side001"
  Group = -> [Sketch025,Pad007,Sketch024,Pocket015,Sketch023,Pocket838,Sketch027,Pocket836,Fillet006,Fillet007,Sketch026,Pocket835,Fillet258,Fillet008]
  Origin = -> Origin009
  Placement = pos=(110,-1.3e-14,-2.4e-14) rot=(0,-1,0;1.5708rad)
  Tip = -> Fillet008
FEATURE [Sketcher::SketchObject] Sketch034
  MapMode = 5
  Support = -> [XY_Plane955]
  sketch-geometry (8):
    g0: LineSegment StartX=0 StartY=3.17543 StartZ=0 EndX=-2.75 EndY=1.58771 EndZ=0
    g1: LineSegment StartX=-2.75 StartY=1.58771 StartZ=0 EndX=-2.75 EndY=-1.58771 EndZ=0
    g2: LineSegment StartX=-2.75 StartY=-1.58771 StartZ=0 EndX=0 EndY=-3.17543 EndZ=0
    g3: LineSegment StartX=0 StartY=-3.17543 StartZ=0 EndX=2.75 EndY=-1.58771 EndZ=0
    g4: LineSegment StartX=2.75 StartY=-1.58771 StartZ=0 EndX=2.75 EndY=1.58771 EndZ=0
    g5: LineSegment StartX=2.75 StartY=1.58771 StartZ=0 EndX=0 EndY=3.17543 EndZ=0
    g6: Circle [constr] CenterX=0 CenterY=0 CenterZ=0 NormalX=0 NormalY=0 NormalZ=1 AngleXU=0 Radius=3.17543
    g7: Circle CenterX=0 CenterY=0 CenterZ=0 NormalX=0 NormalY=0 NormalZ=1 AngleXU=0 Radius=1.5
  constraints (18):
    c: Coincident(g0,g1)
    c: Coincident(g1,g2)
    c: Coincident(g2,g3)
    c: Coincident(g3,g4)
    c: Coincident(g4,g5)
    c: Coincident(g5,g0)
    c: Equal(g0, g1-g5) x5
    c: PointOnObject(g0,g6)
    c: PointOnObject(g1,g6)
    c: PointOnObject(g2,g6)
    c: PointOnObject(g3,g6)
    c: PointOnObject(g4,g6)
    c: PointOnObject(g5,g6)
    c: Coincident(g6,g-1)
    c: PointOnObject(g5,g-2)
    c: DistanceX(g0,g4) = 5.5
    c: Coincident(g7,g-1)
    c: Radius(g7) = 1.5
FEATURE [PartDesign::Pad] Pad1051  label="M3 Nut Primitive005"
  Length = 1.2
  Length2 = 1.2
  Profile = -> Sketch034
  Type = 4
FEATURE [Sketcher::SketchObject] Sketch033
  ExternalGeometry = -> [Pad1051]
  MapMode = 5
  Placement = pos=(0,0,0) rot=(0.57735,0.57735,0.57735;2.0944rad)
  Support = -> [YZ_Plane945]
  sketch-geometry (6):
    g0: LineSegment StartX=-2.67543 StartY=1.2 StartZ=0 EndX=-3.67543 EndY=1.2 EndZ=0
    g1: LineSegment StartX=-3.67543 StartY=1.2 StartZ=0 EndX=-3.67543 EndY=-1.2 EndZ=0
    g2: LineSegment StartX=-3.67543 StartY=-1.2 StartZ=0 EndX=-2.67543 EndY=-1.2 EndZ=0
    g3: LineSegment StartX=-2.67543 StartY=-1.2 StartZ=0 EndX=-3.17543 EndY=-1 EndZ=0
    g4: LineSegment StartX=-3.17543 StartY=-1 StartZ=0 EndX=-3.17543 EndY=1 EndZ=0
    g5: LineSegment StartX=-3.17543 StartY=1 StartZ=0 EndX=-2.67543 EndY=1.2 EndZ=0
  constraints (15):
    c: Horizontal(g0)
    c: Coincident(g0,g1)
    c: Coincident(g1,g2)
    c: Coincident(g2,g3)
    c: Coincident(g3,g4)
    c: Coincident(g4,g5)
    c: Coincident(g5,g0)
    c: Symmetric(g4,g3,g-1)
    c: Symmetric(g0,g2,g-1)
    c: Symmetric(g1,g0,g-1)
    c: DistanceX(g0,g4) = 0.5
    c: DistanceY(g3,g4) = 2
    c: DistanceY(g1,g0) = 2.4
    c: PointOnObject(g3,g-3)
    c: DistanceX(g4,g0) = 0.5
FEATURE [PartDesign::Groove] Groove006  label="M3 Nut Smooth006"
  Angle = 360
  Axis = (-2e-16,3e-16,1)
  Base = (0,0,0)
  BaseFeature = -> Pad1051
  Profile = -> Sketch033
  ReferenceAxis = -> Sketch033 [V_Axis]
  Reversed = true
FEATURE [PartDesign::Chamfer] Chamfer006  label="M3 Nut Smooth Hole005"
  Base = -> Groove006 [Edge24,Edge23]
  BaseFeature = -> Groove006
  Size = 0.2
FEATURE [PartDesign::Body] Body668  label="M3 Nut110"
  Group = -> [Sketch034,Pad1051,Sketch033,Groove006,Chamfer006]
  Origin = -> Origin956
  Placement = pos=(7.5,-70.5,-1.6e-14) rot=(1,0,0;1.5708rad)
  Tip = -> Chamfer006
FEATURE [Sketcher::SketchObject] Sketch035
  MapMode = 5
  Support = -> [XY_Plane944]
  sketch-geometry (8):
    g0: LineSegment StartX=0 StartY=3.17543 StartZ=0 EndX=-2.75 EndY=1.58771 EndZ=0
    g1: LineSegment StartX=-2.75 StartY=1.58771 StartZ=0 EndX=-2.75 EndY=-1.58771 EndZ=0
    g2: LineSegment StartX=-2.75 StartY=-1.58771 StartZ=0 EndX=0 EndY=-3.17543 EndZ=0
    g3: LineSegment StartX=0 StartY=-3.17543 StartZ=0 EndX=2.75 EndY=-1.58771 EndZ=0
    g4: LineSegment StartX=2.75 StartY=-1.58771 StartZ=0 EndX=2.75 EndY=1.58771 EndZ=0
    g5: LineSegment StartX=2.75 StartY=1.58771 StartZ=0 EndX=0 EndY=3.17543 EndZ=0
    g6: Circle [constr] CenterX=0 CenterY=0 CenterZ=0 NormalX=0 NormalY=0 NormalZ=1 AngleXU=0 Radius=3.17543
    g7: Circle CenterX=0 CenterY=0 CenterZ=0 NormalX=0 NormalY=0 NormalZ=1 AngleXU=0 Radius=1.5
  constraints (18):
    c: Coincident(g0,g1)
    c: Coincident(g1,g2)
    c: Coincident(g2,g3)
    c: Coincident(g3,g4)
    c: Coincident(g4,g5)
    c: Coincident(g5,g0)
    c: Equal(g0, g1-g5) x5
    c: PointOnObject(g0,g6)
    c: PointOnObject(g1,g6)
    c: PointOnObject(g2,g6)
    c: PointOnObject(g3,g6)
    c: PointOnObject(g4,g6)
    c: PointOnObject(g5,g6)
    c: Coincident(g6,g-1)
    c: PointOnObject(g5,g-2)
    c: DistanceX(g0,g4) = 5.5
    c: Coincident(g7,g-1)
    c: Radius(g7) = 1.5
FEATURE [PartDesign::Pad] Pad011  label="M3 Nut Primitive211"
  Length = 1.2
  Length2 = 1.2
  Profile = -> Sketch035
  Type = 4
FEATURE [Sketcher::SketchObject] Sketch028
  ExternalGeometry = -> [Pad011]
  MapMode = 5
  Placement = pos=(0,0,0) rot=(0.57735,0.57735,0.57735;2.0944rad)
  Support = -> [YZ_Plane947]
  sketch-geometry (6):
    g0: LineSegment StartX=-2.67543 StartY=1.2 StartZ=0 EndX=-3.67543 EndY=1.2 EndZ=0
    g1: LineSegment StartX=-3.67543 StartY=1.2 StartZ=0 EndX=-3.67543 EndY=-1.2 EndZ=0
    g2: LineSegment StartX=-3.67543 StartY=-1.2 StartZ=0 EndX=-2.67543 EndY=-1.2 EndZ=0
    g3: LineSegment StartX=-2.67543 StartY=-1.2 StartZ=0 EndX=-3.17543 EndY=-1 EndZ=0
    g4: LineSegment StartX=-3.17543 StartY=-1 StartZ=0 EndX=-3.17543 EndY=1 EndZ=0
    g5: LineSegment StartX=-3.17543 StartY=1 StartZ=0 EndX=-2.67543 EndY=1.2 EndZ=0
  constraints (15):
    c: Horizontal(g0)
    c: Coincident(g0,g1)
    c: Coincident(g1,g2)
    c: Coincident(g2,g3)
    c: Coincident(g3,g4)
    c: Coincident(g4,g5)
    c: Coincident(g5,g0)
    c: Symmetric(g4,g3,g-1)
    c: Symmetric(g0,g2,g-1)
    c: Symmetric(g1,g0,g-1)
    c: DistanceX(g0,g4) = 0.5
    c: DistanceY(g3,g4) = 2
    c: DistanceY(g1,g0) = 2.4
    c: PointOnObject(g3,g-3)
    c: DistanceX(g4,g0) = 0.5
FEATURE [PartDesign::Groove] Groove005  label="M3 Nut Smooth005"
  Angle = 360
  Axis = (-2e-16,3e-16,1)
  Base = (0,0,0)
  BaseFeature = -> Pad011
  Profile = -> Sketch028
  ReferenceAxis = -> Sketch028 [V_Axis]
  Reversed = true
FEATURE [PartDesign::Chamfer] Chamfer008  label="M3 Nut Smooth Hole212"
  Base = -> Groove005 [Edge24,Edge23]
  BaseFeature = -> Groove005
  Size = 0.2
FEATURE [PartDesign::Body] Body665  label="M3 Nut108"
  Group = -> [Sketch035,Pad011,Sketch028,Groove005,Chamfer008]
  Origin = -> Origin958
  Placement = pos=(-7.5,70.5,1.6e-14) rot=(1,0,0;1.5708rad)
  Tip = -> Chamfer008
FEATURE [Sketcher::SketchObject] Sketch031
  MapMode = 5
  Support = -> [XY_Plane943]
  sketch-geometry (8):
    g0: LineSegment StartX=0 StartY=3.17543 StartZ=0 EndX=-2.75 EndY=1.58771 EndZ=0
    g1: LineSegment StartX=-2.75 StartY=1.58771 StartZ=0 EndX=-2.75 EndY=-1.58771 EndZ=0
    g2: LineSegment StartX=-2.75 StartY=-1.58771 StartZ=0 EndX=0 EndY=-3.17543 EndZ=0
    g3: LineSegment StartX=0 StartY=-3.17543 StartZ=0 EndX=2.75 EndY=-1.58771 EndZ=0
    g4: LineSegment StartX=2.75 StartY=-1.58771 StartZ=0 EndX=2.75 EndY=1.58771 EndZ=0
    g5: LineSegment StartX=2.75 StartY=1.58771 StartZ=0 EndX=0 EndY=3.17543 EndZ=0
    g6: Circle [constr] CenterX=0 CenterY=0 CenterZ=0 NormalX=0 NormalY=0 NormalZ=1 AngleXU=0 Radius=3.17543
    g7: Circle CenterX=0 CenterY=0 CenterZ=0 NormalX=0 NormalY=0 NormalZ=1 AngleXU=0 Radius=1.5
  constraints (18):
    c: Coincident(g0,g1)
    c: Coincident(g1,g2)
    c: Coincident(g2,g3)
    c: Coincident(g3,g4)
    c: Coincident(g4,g5)
    c: Coincident(g5,g0)
    c: Equal(g0, g1-g5) x5
    c: PointOnObject(g0,g6)
    c: PointOnObject(g1,g6)
    c: PointOnObject(g2,g6)
    c: PointOnObject(g3,g6)
    c: PointOnObject(g4,g6)
    c: PointOnObject(g5,g6)
    c: Coincident(g6,g-1)
    c: PointOnObject(g5,g-2)
    c: DistanceX(g0,g4) = 5.5
    c: Coincident(g7,g-1)
    c: Radius(g7) = 1.5
FEATURE [PartDesign::Pad] Pad010  label="M3 Nut Primitive006"
  Length = 1.2
  Length2 = 1.2
  Profile = -> Sketch031
  Type = 4
FEATURE [Sketcher::SketchObject] Sketch029
  ExternalGeometry = -> [Pad010]
  MapMode = 5
  Placement = pos=(0,0,0) rot=(0.57735,0.57735,0.57735;2.0944rad)
  Support = -> [YZ_Plane950]
  sketch-geometry (6):
    g0: LineSegment StartX=-2.67543 StartY=1.2 StartZ=0 EndX=-3.67543 EndY=1.2 EndZ=0
    g1: LineSegment StartX=-3.67543 StartY=1.2 StartZ=0 EndX=-3.67543 EndY=-1.2 EndZ=0
    g2: LineSegment StartX=-3.67543 StartY=-1.2 StartZ=0 EndX=-2.67543 EndY=-1.2 EndZ=0
    g3: LineSegment StartX=-2.67543 StartY=-1.2 StartZ=0 EndX=-3.17543 EndY=-1 EndZ=0
    g4: LineSegment StartX=-3.17543 StartY=-1 StartZ=0 EndX=-3.17543 EndY=1 EndZ=0
    g5: LineSegment StartX=-3.17543 StartY=1 StartZ=0 EndX=-2.67543 EndY=1.2 EndZ=0
  constraints (15):
    c: Horizontal(g0)
    c: Coincident(g0,g1)
    c: Coincident(g1,g2)
    c: Coincident(g2,g3)
    c: Coincident(g3,g4)
    c: Coincident(g4,g5)
    c: Coincident(g5,g0)
    c: Symmetric(g4,g3,g-1)
    c: Symmetric(g0,g2,g-1)
    c: Symmetric(g1,g0,g-1)
    c: DistanceX(g0,g4) = 0.5
    c: DistanceY(g3,g4) = 2
    c: DistanceY(g1,g0) = 2.4
    c: PointOnObject(g3,g-3)
    c: DistanceX(g4,g0) = 0.5
FEATURE [PartDesign::Groove] Groove219  label="M3 Nut Smooth211"
  Angle = 360
  Axis = (-2e-16,3e-16,1)
  Base = (0,0,0)
  BaseFeature = -> Pad010
  Profile = -> Sketch029
  ReferenceAxis = -> Sketch029 [V_Axis]
  Reversed = true
FEATURE [PartDesign::Chamfer] Chamfer007  label="M3 Nut Smooth Hole006"
  Base = -> Groove219 [Edge24,Edge23]
  BaseFeature = -> Groove219
  Size = 0.2
FEATURE [PartDesign::Body] Body667  label="M3 Nut109"
  Group = -> [Sketch031,Pad010,Sketch029,Groove219,Chamfer007]
  Origin = -> Origin959
  Placement = pos=(7.5,70.5,1.6e-14) rot=(1,0,0;1.5708rad)
  Tip = -> Chamfer007
FEATURE [Sketcher::SketchObject] Sketch032
  ExternalGeometry = -> [Pad1050]
  MapMode = 5
  Placement = pos=(0,0,0) rot=(0.57735,0.57735,0.57735;2.0944rad)
  Support = -> [YZ_Plane946]
  sketch-geometry (6):
    g0: LineSegment StartX=-2.67543 StartY=1.2 StartZ=0 EndX=-3.67543 EndY=1.2 EndZ=0
    g1: LineSegment StartX=-3.67543 StartY=1.2 StartZ=0 EndX=-3.67543 EndY=-1.2 EndZ=0
    g2: LineSegment StartX=-3.67543 StartY=-1.2 StartZ=0 EndX=-2.67543 EndY=-1.2 EndZ=0
    g3: LineSegment StartX=-2.67543 StartY=-1.2 StartZ=0 EndX=-3.17543 EndY=-1 EndZ=0
    g4: LineSegment StartX=-3.17543 StartY=-1 StartZ=0 EndX=-3.17543 EndY=1 EndZ=0
    g5: LineSegment StartX=-3.17543 StartY=1 StartZ=0 EndX=-2.67543 EndY=1.2 EndZ=0
  constraints (15):
    c: Horizontal(g0)
    c: Coincident(g0,g1)
    c: Coincident(g1,g2)
    c: Coincident(g2,g3)
    c: Coincident(g3,g4)
    c: Coincident(g4,g5)
    c: Coincident(g5,g0)
    c: Symmetric(g4,g3,g-1)
    c: Symmetric(g0,g2,g-1)
    c: Symmetric(g1,g0,g-1)
    c: DistanceX(g0,g4) = 0.5
    c: DistanceY(g3,g4) = 2
    c: DistanceY(g1,g0) = 2.4
    c: PointOnObject(g3,g-3)
    c: DistanceX(g4,g0) = 0.5
FEATURE [PartDesign::Groove] Groove004  label="M3 Nut Smooth004"
  Angle = 360
  Axis = (-2e-16,3e-16,1)
  Base = (0,0,0)
  BaseFeature = -> Pad1050
  Profile = -> Sketch032
  ReferenceAxis = -> Sketch032 [V_Axis]
  Reversed = true
FEATURE [PartDesign::Chamfer] Chamfer005  label="M3 Nut Smooth Hole004"
  Base = -> Groove004 [Edge24,Edge23]
  BaseFeature = -> Groove004
  Size = 0.2
FEATURE [PartDesign::Body] Body664  label="M3 Nut107"
  Group = -> [Sketch030,Pad1050,Sketch032,Groove004,Chamfer005]
  Origin = -> Origin010
  Placement = pos=(-7.5,-70.5,-1.6e-14) rot=(1,0,0;1.5708rad)
  Tip = -> Chamfer005
FEATURE [Sketcher::SketchObject] Sketch2380
  MapMode = 5
  Support = -> [XY_Plane953]
  sketch-geometry (4):
    g0: LineSegment StartX=-54 StartY=75 StartZ=0 EndX=54 EndY=75 EndZ=0
    g1: LineSegment StartX=54 StartY=75 StartZ=0 EndX=54 EndY=-75 EndZ=0
    g2: LineSegment StartX=54 StartY=-75 StartZ=0 EndX=-54 EndY=-75 EndZ=0
    g3: LineSegment StartX=-54 StartY=-75 StartZ=0 EndX=-54 EndY=75 EndZ=0
  constraints (10):
    c: Coincident(g0,g1)
    c: Coincident(g1,g2)
    c: Coincident(g2,g3)
    c: Coincident(g3,g0)
    c: Horizontal(g2)
    c: Vertical(g3)
    c: Symmetric(g0,g0,g-2)
    c: Symmetric(g1,g0,g-1)
    c: DistanceX(g0,g0) = 108
    c: DistanceY(g1,g1) = 150
FEATURE [PartDesign::Pad] Pad005  label="Baseplate044"
  Length = 5
  Length2 = 100
  Profile = -> Sketch2380
  Type = 0
FEATURE [Sketcher::SketchObject] Sketch014
  MapMode = 5
  Placement = pos=(0,0,5) rot=(0,0,1;0rad)
  Support = -> [Pad005]
  sketch-geometry (16):
    g0: LineSegment StartX=-55 StartY=75 StartZ=0 EndX=-49.5 EndY=75 EndZ=0
    g1: LineSegment StartX=-49.5 StartY=75 StartZ=0 EndX=-49.5 EndY=59.5 EndZ=0
    g2: LineSegment StartX=-49.5 StartY=59.5 StartZ=0 EndX=-55 EndY=59.5 EndZ=0
    g3: LineSegment StartX=-55 StartY=59.5 StartZ=0 EndX=-55 EndY=75 EndZ=0
    g4: LineSegment StartX=55 StartY=75 StartZ=0 EndX=49.5 EndY=75 EndZ=0
    g5: LineSegment StartX=49.5 StartY=75 StartZ=0 EndX=49.5 EndY=59.5 EndZ=0
    g6: LineSegment StartX=49.5 StartY=59.5 StartZ=0 EndX=55 EndY=59.5 EndZ=0
    g7: LineSegment StartX=55 StartY=59.5 StartZ=0 EndX=55 EndY=75 EndZ=0
    g8: LineSegment StartX=55 StartY=-75 StartZ=0 EndX=49.5 EndY=-75 EndZ=0
    g9: LineSegment StartX=49.5 StartY=-75 StartZ=0 EndX=49.5 EndY=-59.5 EndZ=0
    g10: LineSegment StartX=49.5 StartY=-59.5 StartZ=0 EndX=55 EndY=-59.5 EndZ=0
    g11: LineSegment StartX=55 StartY=-59.5 StartZ=0 EndX=55 EndY=-75 EndZ=0
    g12: LineSegment StartX=-55 StartY=-75 StartZ=0 EndX=-49.5 EndY=-75 EndZ=0
    g13: LineSegment StartX=-49.5 StartY=-75 StartZ=0 EndX=-49.5 EndY=-59.5 EndZ=0
    g14: LineSegment StartX=-49.5 StartY=-59.5 StartZ=0 EndX=-55 EndY=-59.5 EndZ=0
    g15: LineSegment StartX=-55 StartY=-59.5 StartZ=0 EndX=-55 EndY=-75 EndZ=0
  constraints (45):
    c: Coincident(g0,g1)
    c: Coincident(g1,g2)
    c: Coincident(g2,g3)
    c: Coincident(g3,g0)
    c: Horizontal(g0)
    c: Horizontal(g2)
    c: Vertical(g1)
    c: Vertical(g3)
    c: Coincident(g4,g5)
    c: Coincident(g5,g6)
    c: Coincident(g6,g7)
    c: Coincident(g7,g4)
    c: Horizontal(g4)
    c: Horizontal(g6)
    c: Vertical(g5)
    c: Vertical(g7)
    c: Coincident(g8,g9)
    c: Coincident(g9,g10)
    c: Coincident(g10,g11)
    c: Coincident(g11,g8)
    c: Horizontal(g8)
    c: Horizontal(g10)
    c: Vertical(g9)
    c: Vertical(g11)
    c: Coincident(g12,g13)
    c: Coincident(g13,g14)
    c: Coincident(g14,g15)
    c: Coincident(g15,g12)
    c: Horizontal(g12)
    c: Horizontal(g14)
    c: Vertical(g13)
    c: Vertical(g15)
    c: Equal(g2,g14)
    c: Equal(g14,g10)
    c: Equal(g10,g6)
    c: Symmetric(g0,g4,g-2)
    c: Symmetric(g10,g6,g-1)
    c: Symmetric(g2,g14,g-1)
    c: Equal(g1,g13)
    c: Equal(g13,g9)
    c: Equal(g9,g5)
    c: DistanceX(g0,g0) = 5.5
    c: DistanceY(g1,g1) = 15.5
    c: DistanceY(g8,g4) = 150
    c: DistanceX(g0,g4) = 110
FEATURE [PartDesign::Pocket] Pocket839  label="Baseplate Cutout"
  BaseFeature = -> Pad005
  Length = 5
  Length2 = 100
  Profile = -> Sketch014
  Type = 0
FEATURE [PartDesign::Fillet] Fillet004  label="Smooth Baseplate Corners001"
  Base = -> Pocket839 [Edge4,Edge28,Edge29,Edge2,Edge16,Edge36,Edge35,Edge34,Edge33,Edge32,Edge31,Edge30,Face4]
  BaseFeature = -> Pocket839
  Radius = 0.4
FEATURE [Sketcher::SketchObject] Sketch013
  MapMode = 5
  Placement = pos=(0,0,5) rot=(0,0,1;0rad)
  Support = -> [Fillet004]
  sketch-geometry (8):
    g0: ArcOfCircle CenterX=-25 CenterY=-40 CenterZ=0 NormalX=0 NormalY=0 NormalZ=1 AngleXU=0 Radius=15 StartAngle=3.14159 EndAngle=6.28319
    g1: ArcOfCircle CenterX=-25 CenterY=40 CenterZ=0 NormalX=0 NormalY=0 NormalZ=1 AngleXU=0 Radius=15 StartAngle=0 EndAngle=3.14159
    g2: LineSegment StartX=-10 StartY=-40 StartZ=0 EndX=-10 EndY=40 EndZ=0
    g3: LineSegment StartX=-40 StartY=-40 StartZ=0 EndX=-40 EndY=40 EndZ=0
    g4: ArcOfCircle CenterX=25 CenterY=-40 CenterZ=0 NormalX=0 NormalY=0 NormalZ=1 AngleXU=0 Radius=15 StartAngle=3.14159 EndAngle=6.28319
    g5: ArcOfCircle CenterX=25 CenterY=40 CenterZ=0 NormalX=0 NormalY=0 NormalZ=1 AngleXU=0 Radius=15 StartAngle=0 EndAngle=3.14159
    g6: LineSegment StartX=40 StartY=-40 StartZ=0 EndX=40 EndY=40 EndZ=0
    g7: LineSegment StartX=10 StartY=-40 StartZ=0 EndX=10 EndY=40 EndZ=0
  constraints (17):
    c: Tangent(g0,g3) = 1.5708
    c: Tangent(g0,g2) = -1.5708
    c: Tangent(g2,g1) = -1.5708
    c: Tangent(g3,g1) = 1.5708
    c: Vertical(g2)
    c: Tangent(g4,g7) = 1.5708
    c: Tangent(g4,g6) = -1.5708
    c: Tangent(g6,g5) = -1.5708
    c: Tangent(g7,g5) = 1.5708
    c: Vertical(g6)
    c: Equal(g1,g5)
    c: Symmetric(g1,g5,g-2)
    c: Symmetric(g0,g4,g-2)
    c: Radius(g5) = 15
    c: DistanceX(g1,g5) = 50
    c: DistanceY(g4,g5) = 80
    c: Symmetric(g5,g4,g-1)
FEATURE [PartDesign::Pocket] Pocket837  label="Baseplate Weight Reduction"
  BaseFeature = -> Fillet004
  Length = 5
  Length2 = 100
  Profile = -> Sketch013
  Type = 0
FEATURE [PartDesign::Body] Body007  label="Circuitboard Mount (Template)"
  Group = -> [Sketch2380,Pad005,Sketch014,Pocket839,Fillet004,Sketch013,Pocket837]
  Origin = -> Origin955
  Placement = pos=(55,0,-9.75) rot=(0,0,1;0rad)
  Tip = -> Pocket837
FEATURE [Sketcher::SketchObject] Sketch084
  MapMode = 5
  Support = -> [XY_Plane039]
  sketch-geometry (8):
    g0: LineSegment StartX=0 StartY=3.17543 StartZ=0 EndX=-2.75 EndY=1.58771 EndZ=0
    g1: LineSegment StartX=-2.75 StartY=1.58771 StartZ=0 EndX=-2.75 EndY=-1.58771 EndZ=0
    g2: LineSegment StartX=-2.75 StartY=-1.58771 StartZ=0 EndX=0 EndY=-3.17543 EndZ=0
    g3: LineSegment StartX=0 StartY=-3.17543 StartZ=0 EndX=2.75 EndY=-1.58771 EndZ=0
    g4: LineSegment StartX=2.75 StartY=-1.58771 StartZ=0 EndX=2.75 EndY=1.58771 EndZ=0
    g5: LineSegment StartX=2.75 StartY=1.58771 StartZ=0 EndX=0 EndY=3.17543 EndZ=0
    g6: Circle [constr] CenterX=0 CenterY=0 CenterZ=0 NormalX=0 NormalY=0 NormalZ=1 AngleXU=0 Radius=3.17543
    g7: Circle CenterX=0 CenterY=0 CenterZ=0 NormalX=0 NormalY=0 NormalZ=1 AngleXU=0 Radius=1.5
  constraints (18):
    c: Coincident(g0,g1)
    c: Coincident(g1,g2)
    c: Coincident(g2,g3)
    c: Coincident(g3,g4)
    c: Coincident(g4,g5)
    c: Coincident(g5,g0)
    c: Equal(g0, g1-g5) x5
    c: PointOnObject(g0,g6)
    c: PointOnObject(g1,g6)
    c: PointOnObject(g2,g6)
    c: PointOnObject(g3,g6)
    c: PointOnObject(g4,g6)
    c: PointOnObject(g5,g6)
    c: Coincident(g6,g-1)
    c: PointOnObject(g5,g-2)
    c: DistanceX(g0,g4) = 5.5
    c: Coincident(g7,g-1)
    c: Radius(g7) = 1.5
FEATURE [PartDesign::Pad] Pad035  label="M3 Nut Primitive209"
  Length = 1.2
  Length2 = 1.2
  Profile = -> Sketch084
  Type = 4
FEATURE [Sketcher::SketchObject] Sketch080
  ExternalGeometry = -> [Pad035]
  MapMode = 5
  Placement = pos=(0,0,0) rot=(0.57735,0.57735,0.57735;2.0944rad)
  Support = -> [YZ_Plane039]
  sketch-geometry (6):
    g0: LineSegment StartX=-2.67543 StartY=1.2 StartZ=0 EndX=-3.67543 EndY=1.2 EndZ=0
    g1: LineSegment StartX=-3.67543 StartY=1.2 StartZ=0 EndX=-3.67543 EndY=-1.2 EndZ=0
    g2: LineSegment StartX=-3.67543 StartY=-1.2 StartZ=0 EndX=-2.67543 EndY=-1.2 EndZ=0
    g3: LineSegment StartX=-2.67543 StartY=-1.2 StartZ=0 EndX=-3.17543 EndY=-1 EndZ=0
    g4: LineSegment StartX=-3.17543 StartY=-1 StartZ=0 EndX=-3.17543 EndY=1 EndZ=0
    g5: LineSegment StartX=-3.17543 StartY=1 StartZ=0 EndX=-2.67543 EndY=1.2 EndZ=0
  constraints (15):
    c: Horizontal(g0)
    c: Coincident(g0,g1)
    c: Coincident(g1,g2)
    c: Coincident(g2,g3)
    c: Coincident(g3,g4)
    c: Coincident(g4,g5)
    c: Coincident(g5,g0)
    c: Symmetric(g4,g3,g-1)
    c: Symmetric(g0,g2,g-1)
    c: Symmetric(g1,g0,g-1)
    c: DistanceX(g0,g4) = 0.5
    c: DistanceY(g3,g4) = 2
    c: DistanceY(g1,g0) = 2.4
    c: PointOnObject(g3,g-3)
    c: DistanceX(g4,g0) = 0.5
FEATURE [PartDesign::Groove] Groove215  label="M3 Nut Smooth207"
  Angle = 360
  Axis = (-2e-16,3e-16,1)
  Base = (0,0,0)
  BaseFeature = -> Pad035
  Profile = -> Sketch080
  ReferenceAxis = -> Sketch080 [V_Axis]
  Reversed = true
FEATURE [PartDesign::Chamfer] Chamfer518  label="M3 Nut Smooth Hole211"
  Base = -> Groove215 [Edge24,Edge23]
  BaseFeature = -> Groove215
  Size = 0.2
FEATURE [PartDesign::Body] Body029  label="M3 Nut015"
  Group = -> [Sketch084,Pad035,Sketch080,Groove215,Chamfer518]
  Origin = -> Origin039
  Placement = pos=(-15,-110.75,66) rot=(1,0,0;1.5708rad)
  Tip = -> Chamfer518
FEATURE [Sketcher::SketchObject] Sketch083
  MapMode = 5
  Support = -> [XY_Plane041]
  sketch-geometry (8):
    g0: LineSegment StartX=0 StartY=3.17543 StartZ=0 EndX=-2.75 EndY=1.58771 EndZ=0
    g1: LineSegment StartX=-2.75 StartY=1.58771 StartZ=0 EndX=-2.75 EndY=-1.58771 EndZ=0
    g2: LineSegment StartX=-2.75 StartY=-1.58771 StartZ=0 EndX=0 EndY=-3.17543 EndZ=0
    g3: LineSegment StartX=0 StartY=-3.17543 StartZ=0 EndX=2.75 EndY=-1.58771 EndZ=0
    g4: LineSegment StartX=2.75 StartY=-1.58771 StartZ=0 EndX=2.75 EndY=1.58771 EndZ=0
    g5: LineSegment StartX=2.75 StartY=1.58771 StartZ=0 EndX=0 EndY=3.17543 EndZ=0
    g6: Circle [constr] CenterX=0 CenterY=0 CenterZ=0 NormalX=0 NormalY=0 NormalZ=1 AngleXU=0 Radius=3.17543
    g7: Circle CenterX=0 CenterY=0 CenterZ=0 NormalX=0 NormalY=0 NormalZ=1 AngleXU=0 Radius=1.5
  constraints (18):
    c: Coincident(g0,g1)
    c: Coincident(g1,g2)
    c: Coincident(g2,g3)
    c: Coincident(g3,g4)
    c: Coincident(g4,g5)
    c: Coincident(g5,g0)
    c: Equal(g0, g1-g5) x5
    c: PointOnObject(g0,g6)
    c: PointOnObject(g1,g6)
    c: PointOnObject(g2,g6)
    c: PointOnObject(g3,g6)
    c: PointOnObject(g4,g6)
    c: PointOnObject(g5,g6)
    c: Coincident(g6,g-1)
    c: PointOnObject(g5,g-2)
    c: DistanceX(g0,g4) = 5.5
    c: Coincident(g7,g-1)
    c: Radius(g7) = 1.5
FEATURE [PartDesign::Pad] Pad1041  label="M3 Nut Primitive208"
  Length = 1.2
  Length2 = 1.2
  Profile = -> Sketch083
  Type = 4
FEATURE [Sketcher::SketchObject] Sketch087
  ExternalGeometry = -> [Pad1041]
  MapMode = 5
  Placement = pos=(0,0,0) rot=(0.57735,0.57735,0.57735;2.0944rad)
  Support = -> [YZ_Plane042]
  sketch-geometry (6):
    g0: LineSegment StartX=-2.67543 StartY=1.2 StartZ=0 EndX=-3.67543 EndY=1.2 EndZ=0
    g1: LineSegment StartX=-3.67543 StartY=1.2 StartZ=0 EndX=-3.67543 EndY=-1.2 EndZ=0
    g2: LineSegment StartX=-3.67543 StartY=-1.2 StartZ=0 EndX=-2.67543 EndY=-1.2 EndZ=0
    g3: LineSegment StartX=-2.67543 StartY=-1.2 StartZ=0 EndX=-3.17543 EndY=-1 EndZ=0
    g4: LineSegment StartX=-3.17543 StartY=-1 StartZ=0 EndX=-3.17543 EndY=1 EndZ=0
    g5: LineSegment StartX=-3.17543 StartY=1 StartZ=0 EndX=-2.67543 EndY=1.2 EndZ=0
  constraints (15):
    c: Horizontal(g0)
    c: Coincident(g0,g1)
    c: Coincident(g1,g2)
    c: Coincident(g2,g3)
    c: Coincident(g3,g4)
    c: Coincident(g4,g5)
    c: Coincident(g5,g0)
    c: Symmetric(g4,g3,g-1)
    c: Symmetric(g0,g2,g-1)
    c: Symmetric(g1,g0,g-1)
    c: DistanceX(g0,g4) = 0.5
    c: DistanceY(g3,g4) = 2
    c: DistanceY(g1,g0) = 2.4
    c: PointOnObject(g3,g-3)
    c: DistanceX(g4,g0) = 0.5
FEATURE [PartDesign::Groove] Groove216  label="M3 Nut Smooth208"
  Angle = 360
  Axis = (-2e-16,3e-16,1)
  Base = (0,0,0)
  BaseFeature = -> Pad1041
  Profile = -> Sketch087
  ReferenceAxis = -> Sketch087 [V_Axis]
  Reversed = true
FEATURE [PartDesign::Chamfer] Chamfer517  label="M3 Nut Smooth Hole210"
  Base = -> Groove216 [Edge24,Edge23]
  BaseFeature = -> Groove216
  Size = 0.2
FEATURE [PartDesign::Body] Body670  label="M3 Nut014"
  Group = -> [Sketch083,Pad1041,Sketch087,Groove216,Chamfer517]
  Origin = -> Origin035
  Placement = pos=(15,-110.75,66) rot=(1,0,0;1.5708rad)
  Tip = -> Chamfer517
FEATURE [PartDesign::Chamfer] Chamfer520  label="M3x8 Smooth160"
  Base = -> Pocket833 [Face11,Edge2,Edge24,Edge3]
  BaseFeature = -> Pocket833
  Size = 0.2
FEATURE [PartDesign::Chamfer] Chamfer521  label="M3x8 Smooth161"
  Base = -> Pocket831 [Face11,Edge2,Edge24,Edge3]
  BaseFeature = -> Pocket831
  Size = 0.2
FEATURE [PartDesign::Body] Body034  label="M3x131"
  Group = -> [Sketch113,Pad043,Sketch114,Pad044,Sketch112,Pocket831,Chamfer521]
  Origin = -> Origin044
  Placement = pos=(3.25,-2e-15,-7.5) rot=(-1,0,0;1.5708rad)
  Tip = -> Chamfer521
FEATURE [PartDesign::Body] Body674  label="M3x132"
  Group = -> [Sketch2368,Pad1043,Sketch2369,Pad1048,Sketch2367,Pocket830,Chamfer504]
  Origin = -> Origin047
  Placement = pos=(3.25,-2e-15,7.5) rot=(1,0,0;1.5708rad)
  Tip = -> Chamfer504
FEATURE [PartDesign::Body] Body036  label="M3x133"
  Group = -> [Sketch2364,Pad1046,Sketch2372,Pad1044,Sketch2371,Pocket834,Chamfer506]
  Origin = -> Origin046
  Placement = pos=(106.75,-2e-15,-7.5) rot=(-1,0,0;1.5708rad)
  Tip = -> Chamfer506
FEATURE [PartDesign::Body] Body675  label="M3x023"
  Group = -> [Sketch2377,Pad055,Sketch2375,Pad056,Sketch2379,Pocket840,Chamfer503]
  Origin = -> Origin050
  Placement = pos=(106.75,2e-15,-7.5) rot=(1,0,0;1.5708rad)
  Tip = -> Chamfer503
FEATURE [PartDesign::Body] Body676  label="M3x022"
  Group = -> [Sketch2376,Pad1042,Sketch2378,Pad054,Sketch2366,Pocket833,Chamfer520]
  Origin = -> Origin049
  Placement = pos=(106.75,-2e-15,7.5) rot=(1,0,0;1.5708rad)
  Tip = -> Chamfer520
FEATURE [PartDesign::Body] Body677  label="M3x134"
  Group = -> [Sketch2365,Pad1045,Sketch2374,Pad1049,Sketch2373,Pocket832,Chamfer505]
  Origin = -> Origin048
  Placement = pos=(3.25,2e-15,-7.5) rot=(1,0,0;1.5708rad)
  Tip = -> Chamfer505
FEATURE [Sketcher::SketchObject] Sketch085
  ExternalGeometry = -> [Pad040]
  MapMode = 5
  Placement = pos=(0,0,0) rot=(0.57735,0.57735,0.57735;2.0944rad)
  Support = -> [YZ_Plane944]
  sketch-geometry (6):
    g0: LineSegment StartX=-2.67543 StartY=1.2 StartZ=0 EndX=-3.67543 EndY=1.2 EndZ=0
    g1: LineSegment StartX=-3.67543 StartY=1.2 StartZ=0 EndX=-3.67543 EndY=-1.2 EndZ=0
    g2: LineSegment StartX=-3.67543 StartY=-1.2 StartZ=0 EndX=-2.67543 EndY=-1.2 EndZ=0
    g3: LineSegment StartX=-2.67543 StartY=-1.2 StartZ=0 EndX=-3.17543 EndY=-1 EndZ=0
    g4: LineSegment StartX=-3.17543 StartY=-1 StartZ=0 EndX=-3.17543 EndY=1 EndZ=0
    g5: LineSegment StartX=-3.17543 StartY=1 StartZ=0 EndX=-2.67543 EndY=1.2 EndZ=0
  constraints (15):
    c: Horizontal(g0)
    c: Coincident(g0,g1)
    c: Coincident(g1,g2)
    c: Coincident(g2,g3)
    c: Coincident(g3,g4)
    c: Coincident(g4,g5)
    c: Coincident(g5,g0)
    c: Symmetric(g4,g3,g-1)
    c: Symmetric(g0,g2,g-1)
    c: Symmetric(g1,g0,g-1)
    c: DistanceX(g0,g4) = 0.5
    c: DistanceY(g3,g4) = 2
    c: DistanceY(g1,g0) = 2.4
    c: PointOnObject(g3,g-3)
    c: DistanceX(g4,g0) = 0.5
FEATURE [PartDesign::Groove] Groove217  label="M3 Nut Smooth209"
  Angle = 360
  Axis = (-2e-16,3e-16,1)
  Base = (0,0,0)
  BaseFeature = -> Pad040
  Profile = -> Sketch085
  ReferenceAxis = -> Sketch085 [V_Axis]
  Reversed = true
FEATURE [PartDesign::Chamfer] Chamfer514  label="M3 Nut Smooth Hole209"
  Base = -> Groove217 [Edge24,Edge23]
  BaseFeature = -> Groove217
  Size = 0.2
FEATURE [PartDesign::Body] Body023  label="M3 Nut111"
  Group = -> [Sketch070,Pad040,Sketch085,Groove217,Chamfer514]
  Origin = -> Origin042
  Placement = pos=(5,-35.75,6) rot=(1,0,0;1.5708rad)
  Tip = -> Chamfer514
FEATURE [App::Part] Part001  label="Chassis Right Side Nuts001"
  Group = -> [Body664,Body668,Body667,Body665]
  Origin = -> Origin957
  Placement = pos=(106.75,0,-2.48e-14) rot=(0,1,0;1.5708rad)
FEATURE [App::Part] Part011
  Group = -> [Body674,Body677,Body676,Body675]
  Origin = -> Origin052
  Placement = pos=(0,80,0) rot=(0,0,1;0rad)
FEATURE [App::Part] Part265  label="Top SHoulder"
  Group = -> [Body661,Body019,Body660]
  Origin = -> Origin962
  Placement = pos=(-1.62e-14,101.25,130.25) rot=(0,1,0;3.14159rad)
FEATURE [App::Part] Part010
  Group = -> [Body033,Body034,Body035,Body036]
  Origin = -> Origin051
  Placement = pos=(0,-80,0) rot=(0,0,1;0rad)
FEATURE [App::Part] Part266
  Group = -> [Body662,Body669,Body663,Body014]
  Origin = -> Origin021
FEATURE [App::Part] Part008
  Group = -> [Body030,Body032,Body031,Body026]
  Origin = -> Origin034
FEATURE [App::Part] Part267  label="Bototm Shoudler"
  Group = -> [Body659,Body656,Body657]
  Origin = -> Origin946
  Placement = pos=(0,26.2,0) rot=(0,0,1;0rad)
FEATURE [App::Part] Part005  label="Rear Inner SHoulder Assembly"
  Group = -> [Body658,Part267,Part265,Part266]
  Origin = -> Origin026
  Placement = pos=(55,-75,-37.5) rot=(0,0,1;0rad)
FEATURE [Sketcher::SketchObject] Sketch077
  MapMode = 5
  Placement = pos=(0,-23.75,0) rot=(1,0,0;1.5708rad)
  Support = -> [Pad1039]
  sketch-geometry (2):
    g0: Circle CenterX=-15 CenterY=6 CenterZ=0 NormalX=0 NormalY=0 NormalZ=1 AngleXU=0 Radius=1.6
    g1: Circle CenterX=15 CenterY=6 CenterZ=0 NormalX=0 NormalY=0 NormalZ=1 AngleXU=0 Radius=1.6
  constraints (5):
    c: Symmetric(g0,g1,g-2)
    c: Equal(g0,g1)
    c: Radius(g1) = 1.6
    c: DistanceY(g-1,g0) = 6
    c: DistanceX(g0,g1) = 30
FEATURE [PartDesign::Pocket] Pocket826  label="Screwholes Front005"
  BaseFeature = -> Pad1039
  Length = 10
  Length2 = 100
  Profile = -> Sketch077
  Type = 0
FEATURE [Sketcher::SketchObject] Sketch071
  MapMode = 5
  Placement = pos=(0,23.75,0) rot=(0,0.707107,0.707107;3.14159rad)
  Support = -> [Pocket826]
  sketch-geometry (2):
    g0: Circle CenterX=-15 CenterY=6 CenterZ=0 NormalX=0 NormalY=0 NormalZ=1 AngleXU=0 Radius=1.6
    g1: Circle CenterX=15 CenterY=6 CenterZ=0 NormalX=0 NormalY=0 NormalZ=1 AngleXU=0 Radius=1.6
  constraints (5):
    c: Symmetric(g0,g1,g-2)
    c: Equal(g0,g1)
    c: Radius(g1) = 1.6
    c: DistanceY(g-1,g0) = 6
    c: DistanceX(g0,g1) = 30
FEATURE [PartDesign::Pocket] Pocket034  label="Screwholes Rear004"
  BaseFeature = -> Pocket826
  Length = 10
  Length2 = 100
  Profile = -> Sketch071
  Type = 0
FEATURE [Sketcher::SketchObject] Sketch074
  MapMode = 5
  Placement = pos=(0,0,12) rot=(0,0,1;0rad)
  Support = -> [Pocket034]
  sketch-geometry (16):
    g0: LineSegment StartX=-17.9 StartY=20.75 StartZ=0 EndX=-12.1 EndY=20.75 EndZ=0
    g1: LineSegment StartX=-12.1 StartY=20.75 StartZ=0 EndX=-12.1 EndY=17.75 EndZ=0
    g2: LineSegment StartX=-12.1 StartY=17.75 StartZ=0 EndX=-17.9 EndY=17.75 EndZ=0
    g3: LineSegment StartX=-17.9 StartY=17.75 StartZ=0 EndX=-17.9 EndY=20.75 EndZ=0
    g4: LineSegment StartX=12.1 StartY=20.75 StartZ=0 EndX=17.9 EndY=20.75 EndZ=0
    g5: LineSegment StartX=17.9 StartY=20.75 StartZ=0 EndX=17.9 EndY=17.75 EndZ=0
    g6: LineSegment StartX=17.9 StartY=17.75 StartZ=0 EndX=12.1 EndY=17.75 EndZ=0
    g7: LineSegment StartX=12.1 StartY=17.75 StartZ=0 EndX=12.1 EndY=20.75 EndZ=0
    g8: LineSegment StartX=-17.9 StartY=-17.75 StartZ=0 EndX=-12.1 EndY=-17.75 EndZ=0
    g9: LineSegment StartX=-12.1 StartY=-17.75 StartZ=0 EndX=-12.1 EndY=-20.75 EndZ=0
    g10: LineSegment StartX=-12.1 StartY=-20.75 StartZ=0 EndX=-17.9 EndY=-20.75 EndZ=0
    g11: LineSegment StartX=-17.9 StartY=-20.75 StartZ=0 EndX=-17.9 EndY=-17.75 EndZ=0
    g12: LineSegment StartX=12.1 StartY=-17.75 StartZ=0 EndX=17.9 EndY=-17.75 EndZ=0
    g13: LineSegment StartX=17.9 StartY=-17.75 StartZ=0 EndX=17.9 EndY=-20.75 EndZ=0
    g14: LineSegment StartX=17.9 StartY=-20.75 StartZ=0 EndX=12.1 EndY=-20.75 EndZ=0
    g15: LineSegment StartX=12.1 StartY=-20.75 StartZ=0 EndX=12.1 EndY=-17.75 EndZ=0
  constraints (45):
    c: Coincident(g0,g1)
    c: Coincident(g1,g2)
    c: Coincident(g2,g3)
    c: Coincident(g3,g0)
    c: Horizontal(g0)
    c: Horizontal(g2)
    c: Vertical(g1)
    c: Vertical(g3)
    c: Coincident(g4,g5)
    c: Coincident(g5,g6)
    c: Coincident(g6,g7)
    c: Coincident(g7,g4)
    c: Horizontal(g4)
    c: Horizontal(g6)
    c: Vertical(g5)
    c: Vertical(g7)
    c: Coincident(g8,g9)
    c: Coincident(g9,g10)
    c: Coincident(g10,g11)
    c: Coincident(g11,g8)
    c: Horizontal(g8)
    c: Horizontal(g10)
    c: Vertical(g9)
    c: Vertical(g11)
    c: Coincident(g12,g13)
    c: Coincident(g13,g14)
    c: Coincident(g14,g15)
    c: Coincident(g15,g12)
    c: Horizontal(g12)
    c: Horizontal(g14)
    c: Vertical(g13)
    c: Vertical(g15)
    c: Equal(g11,g13)
    c: Equal(g13,g5)
    c: Equal(g5,g3)
    c: Equal(g0,g4)
    c: Equal(g4,g10)
    c: Equal(g10,g14)
    c: DistanceX(g0,g0) = 5.8
    c: Symmetric(g0,g4,g-2)
    c: Symmetric(g9,g14,g-2)
    c: Symmetric(g12,g5,g-1)
    c: DistanceY(g10,g-1) = 20.75
    c: DistanceY(g11,g11) = 3
    c: DistanceX(g0,g4) = 24.2
FEATURE [PartDesign::Pocket] Pocket047  label="Nutholes Front and Rear005"
  BaseFeature = -> Pocket034
  Length = 12
  Length2 = 100
  Profile = -> Sketch074
  Type = 0
FEATURE [Sketcher::SketchObject] Sketch076
  MapMode = 5
  Support = -> [XY_Plane946]
  sketch-geometry (4):
    g0: LineSegment StartX=-10 StartY=23.75 StartZ=0 EndX=10 EndY=23.75 EndZ=0
    g1: LineSegment StartX=10 StartY=23.75 StartZ=0 EndX=10 EndY=-23.75 EndZ=0
    g2: LineSegment StartX=10 StartY=-23.75 StartZ=0 EndX=-10 EndY=-23.75 EndZ=0
    g3: LineSegment StartX=-10 StartY=-23.75 StartZ=0 EndX=-10 EndY=23.75 EndZ=0
  constraints (10):
    c: Coincident(g0,g1)
    c: Coincident(g1,g2)
    c: Coincident(g2,g3)
    c: Coincident(g3,g0)
    c: Horizontal(g2)
    c: Vertical(g1)
    c: Symmetric(g0,g0,g-2)
    c: Symmetric(g0,g2,g-1)
    c: DistanceX(g0,g0) = 20
    c: DistanceY(g3,g3) = 47.5
FEATURE [PartDesign::Pad] Pad1037  label="Baseplate008"
  Length = 12
  Length2 = 100
  Profile = -> Sketch076
  Type = 0
FEATURE [Sketcher::SketchObject] Sketch072
  MapMode = 5
  Placement = pos=(0,-23.75,0) rot=(1,0,0;1.5708rad)
  Support = -> [Pad1037]
  sketch-geometry (2):
    g0: Circle CenterX=-5 CenterY=6 CenterZ=0 NormalX=0 NormalY=0 NormalZ=1 AngleXU=0 Radius=1.6
    g1: Circle CenterX=5 CenterY=6 CenterZ=0 NormalX=0 NormalY=0 NormalZ=1 AngleXU=0 Radius=1.6
  constraints (5):
    c: Symmetric(g0,g1,g-2)
    c: Equal(g0,g1)
    c: Radius(g1) = 1.6
    c: DistanceY(g-1,g0) = 6
    c: DistanceX(g0,g1) = 10
FEATURE [PartDesign::Pocket] Pocket038  label="Screwholes Front004"
  BaseFeature = -> Pad1037
  Length = 10
  Length2 = 100
  Profile = -> Sketch072
  Type = 0
FEATURE [Sketcher::SketchObject] Sketch095
  MapMode = 5
  Placement = pos=(0,23.75,0) rot=(0,0.707107,0.707107;3.14159rad)
  Support = -> [Pocket038]
  sketch-geometry (2):
    g0: Circle CenterX=-5 CenterY=6 CenterZ=0 NormalX=0 NormalY=0 NormalZ=1 AngleXU=0 Radius=1.6
    g1: Circle CenterX=5 CenterY=6 CenterZ=0 NormalX=0 NormalY=0 NormalZ=1 AngleXU=0 Radius=1.6
  constraints (5):
    c: Symmetric(g0,g1,g-2)
    c: Equal(g0,g1)
    c: Radius(g1) = 1.6
    c: DistanceY(g-1,g0) = 6
    c: DistanceX(g0,g1) = 10
FEATURE [PartDesign::Pocket] Pocket044  label="Screwholes Rear005"
  BaseFeature = -> Pocket038
  Length = 10
  Length2 = 100
  Profile = -> Sketch095
  Type = 0
FEATURE [Sketcher::SketchObject] Sketch107
  MapMode = 5
  Placement = pos=(0,0,12) rot=(0,0,1;0rad)
  Support = -> [Pocket044]
  sketch-geometry (16):
    g0: LineSegment StartX=-7.9 StartY=20.75 StartZ=0 EndX=-2.1 EndY=20.75 EndZ=0
    g1: LineSegment StartX=-2.1 StartY=20.75 StartZ=0 EndX=-2.1 EndY=17.75 EndZ=0
    g2: LineSegment StartX=-2.1 StartY=17.75 StartZ=0 EndX=-7.9 EndY=17.75 EndZ=0
    g3: LineSegment StartX=-7.9 StartY=17.75 StartZ=0 EndX=-7.9 EndY=20.75 EndZ=0
    g4: LineSegment StartX=2.1 StartY=20.75 StartZ=0 EndX=7.9 EndY=20.75 EndZ=0
    g5: LineSegment StartX=7.9 StartY=20.75 StartZ=0 EndX=7.9 EndY=17.75 EndZ=0
    g6: LineSegment StartX=7.9 StartY=17.75 StartZ=0 EndX=2.1 EndY=17.75 EndZ=0
    g7: LineSegment StartX=2.1 StartY=17.75 StartZ=0 EndX=2.1 EndY=20.75 EndZ=0
    g8: LineSegment StartX=-7.9 StartY=-17.75 StartZ=0 EndX=-2.1 EndY=-17.75 EndZ=0
    g9: LineSegment StartX=-2.1 StartY=-17.75 StartZ=0 EndX=-2.1 EndY=-20.75 EndZ=0
    g10: LineSegment StartX=-2.1 StartY=-20.75 StartZ=0 EndX=-7.9 EndY=-20.75 EndZ=0
    g11: LineSegment StartX=-7.9 StartY=-20.75 StartZ=0 EndX=-7.9 EndY=-17.75 EndZ=0
    g12: LineSegment StartX=2.1 StartY=-17.75 StartZ=0 EndX=7.9 EndY=-17.75 EndZ=0
    g13: LineSegment StartX=7.9 StartY=-17.75 StartZ=0 EndX=7.9 EndY=-20.75 EndZ=0
    g14: LineSegment StartX=7.9 StartY=-20.75 StartZ=0 EndX=2.1 EndY=-20.75 EndZ=0
    g15: LineSegment StartX=2.1 StartY=-20.75 StartZ=0 EndX=2.1 EndY=-17.75 EndZ=0
  constraints (45):
    c: Coincident(g0,g1)
    c: Coincident(g1,g2)
    c: Coincident(g2,g3)
    c: Coincident(g3,g0)
    c: Horizontal(g0)
    c: Horizontal(g2)
    c: Vertical(g1)
    c: Vertical(g3)
    c: Coincident(g4,g5)
    c: Coincident(g5,g6)
    c: Coincident(g6,g7)
    c: Coincident(g7,g4)
    c: Horizontal(g4)
    c: Horizontal(g6)
    c: Vertical(g5)
    c: Vertical(g7)
    c: Coincident(g8,g9)
    c: Coincident(g9,g10)
    c: Coincident(g10,g11)
    c: Coincident(g11,g8)
    c: Horizontal(g8)
    c: Horizontal(g10)
    c: Vertical(g9)
    c: Vertical(g11)
    c: Coincident(g12,g13)
    c: Coincident(g13,g14)
    c: Coincident(g14,g15)
    c: Coincident(g15,g12)
    c: Horizontal(g12)
    c: Horizontal(g14)
    c: Vertical(g13)
    c: Vertical(g15)
    c: Equal(g11,g13)
    c: Equal(g13,g5)
    c: Equal(g5,g3)
    c: Equal(g0,g4)
    c: Equal(g4,g10)
    c: Equal(g10,g14)
    c: DistanceX(g0,g0) = 5.8
    c: Symmetric(g0,g4,g-2)
    c: Symmetric(g9,g14,g-2)
    c: Symmetric(g12,g5,g-1)
    c: DistanceY(g10,g-1) = 20.75
    c: DistanceY(g11,g11) = 3
    c: DistanceX(g0,g4) = 4.2
FEATURE [PartDesign::Pocket] Pocket035  label="Nutholes Front and Rear004"
  BaseFeature = -> Pocket044
  Length = 12
  Length2 = 100
  Profile = -> Sketch107
  Type = 0
FEATURE [Sketcher::SketchObject] Sketch093
  MapMode = 5
  Placement = pos=(0,0,12) rot=(0,0,1;0rad)
  Support = -> [Pocket035]
  sketch-geometry (4):
    g0: Circle CenterX=-5 CenterY=5 CenterZ=0 NormalX=0 NormalY=0 NormalZ=1 AngleXU=0 Radius=1.6
    g1: Circle CenterX=5 CenterY=5 CenterZ=0 NormalX=0 NormalY=0 NormalZ=1 AngleXU=0 Radius=1.6
    g2: Circle CenterX=-5 CenterY=-5 CenterZ=0 NormalX=0 NormalY=0 NormalZ=1 AngleXU=0 Radius=1.6
    g3: Circle CenterX=5 CenterY=-5 CenterZ=0 NormalX=0 NormalY=0 NormalZ=1 AngleXU=0 Radius=1.6
  constraints (9):
    c: Equal(g0,g1)
    c: Equal(g1,g2)
    c: Equal(g2,g3)
    c: Symmetric(g3,g1,g-1)
    c: Symmetric(g0,g1,g-2)
    c: Symmetric(g2,g3,g-2)
    c: Radius(g1) = 1.6
    c: DistanceX(g0,g1) = 10
    c: DistanceY(g2,g0) = 10
FEATURE [PartDesign::Pocket] Pocket045  label="Screwholes Covers002"
  BaseFeature = -> Pocket035
  Length = 12
  Length2 = 100
  Profile = -> Sketch093
  Type = 0
FEATURE [Sketcher::SketchObject] Sketch108
  ExternalGeometry = -> [Pocket045]
  MapMode = 5
  Placement = pos=(0,0,12) rot=(0,0,1;0rad)
  Support = -> [Pocket045]
  sketch-geometry (28):
    g0: LineSegment StartX=-5 StartY=8.2909 StartZ=0 EndX=-7.85 EndY=6.64545 EndZ=0
    g1: LineSegment StartX=-7.85 StartY=6.64545 StartZ=0 EndX=-7.85 EndY=3.35455 EndZ=0
    g2: LineSegment StartX=-7.85 StartY=3.35455 StartZ=0 EndX=-5 EndY=1.7091 EndZ=0
    g3: LineSegment StartX=-5 StartY=1.7091 StartZ=0 EndX=-2.15 EndY=3.35455 EndZ=0
    g4: LineSegment StartX=-2.15 StartY=3.35455 StartZ=0 EndX=-2.15 EndY=6.64545 EndZ=0
    g5: LineSegment StartX=-2.15 StartY=6.64545 StartZ=0 EndX=-5 EndY=8.2909 EndZ=0
    g6: Circle [constr] CenterX=-5 CenterY=5 CenterZ=0 NormalX=0 NormalY=0 NormalZ=1 AngleXU=0 Radius=3.2909
    g7: LineSegment StartX=7.85 StartY=6.64545 StartZ=0 EndX=5 EndY=8.2909 EndZ=0
    g8: LineSegment StartX=5 StartY=8.2909 StartZ=0 EndX=2.15 EndY=6.64545 EndZ=0
    g9: LineSegment StartX=2.15 StartY=6.64545 StartZ=0 EndX=2.15 EndY=3.35455 EndZ=0
    g10: LineSegment StartX=2.15 StartY=3.35455 StartZ=0 EndX=5 EndY=1.7091 EndZ=0
    g11: LineSegment StartX=5 StartY=1.7091 StartZ=0 EndX=7.85 EndY=3.35455 EndZ=0
    g12: LineSegment StartX=7.85 StartY=3.35455 StartZ=0 EndX=7.85 EndY=6.64545 EndZ=0
    g13: Circle [constr] CenterX=5 CenterY=5 CenterZ=0 NormalX=0 NormalY=0 NormalZ=1 AngleXU=0 Radius=3.2909
    g14: LineSegment StartX=-5 StartY=-1.7091 StartZ=0 EndX=-7.85 EndY=-3.35455 EndZ=0
    g15: LineSegment StartX=-7.85 StartY=-3.35455 StartZ=0 EndX=-7.85 EndY=-6.64545 EndZ=0
    g16: LineSegment StartX=-7.85 StartY=-6.64545 StartZ=0 EndX=-5 EndY=-8.2909 EndZ=0
    g17: LineSegment StartX=-5 StartY=-8.2909 StartZ=0 EndX=-2.15 EndY=-6.64545 EndZ=0
    g18: LineSegment StartX=-2.15 StartY=-6.64545 StartZ=0 EndX=-2.15 EndY=-3.35455 EndZ=0
    g19: LineSegment StartX=-2.15 StartY=-3.35455 StartZ=0 EndX=-5 EndY=-1.7091 EndZ=0
    g20: Circle [constr] CenterX=-5 CenterY=-5 CenterZ=0 NormalX=0 NormalY=0 NormalZ=1 AngleXU=0 Radius=3.2909
    g21: LineSegment StartX=7.85 StartY=-3.35455 StartZ=0 EndX=5 EndY=-1.7091 EndZ=0
    g22: LineSegment StartX=5 StartY=-1.7091 StartZ=0 EndX=2.15 EndY=-3.35455 EndZ=0
    g23: LineSegment StartX=2.15 StartY=-3.35455 StartZ=0 EndX=2.15 EndY=-6.64545 EndZ=0
    g24: LineSegment StartX=2.15 StartY=-6.64545 StartZ=0 EndX=5 EndY=-8.2909 EndZ=0
    g25: LineSegment StartX=5 StartY=-8.2909 StartZ=0 EndX=7.85 EndY=-6.64545 EndZ=0
    g26: LineSegment StartX=7.85 StartY=-6.64545 StartZ=0 EndX=7.85 EndY=-3.35455 EndZ=0
    g27: Circle [constr] CenterX=5 CenterY=-5 CenterZ=0 NormalX=0 NormalY=0 NormalZ=1 AngleXU=0 Radius=3.2909
  constraints (64):
    c: Coincident(g0,g1)
    c: Coincident(g1,g2)
    c: Coincident(g2,g3)
    c: Coincident(g3,g4)
    c: Coincident(g4,g5)
    c: Coincident(g5,g0)
    c: Equal(g0, g1-g5) x5
    c: PointOnObject(g0,g6)
    c: PointOnObject(g1,g6)
    c: PointOnObject(g2,g6)
    c: PointOnObject(g3,g6)
    c: PointOnObject(g4,g6)
    c: PointOnObject(g5,g6)
    c: Coincident(g7,g8)
    c: Coincident(g8,g9)
    c: Coincident(g9,g10)
    c: Coincident(g10,g11)
    c: Coincident(g11,g12)
    c: Coincident(g12,g7)
    c: Equal(g7, g8-g12) x5
    c: PointOnObject(g7,g13)
    c: PointOnObject(g8,g13)
    c: PointOnObject(g9,g13)
    c: PointOnObject(g10,g13)
    c: PointOnObject(g11,g13)
    c: PointOnObject(g12,g13)
    c: Coincident(g14,g15)
    c: Coincident(g15,g16)
    c: Coincident(g16,g17)
    c: Coincident(g17,g18)
    c: Coincident(g18,g19)
    c: Coincident(g19,g14)
    c: Equal(g14, g15-g19) x5
    c: PointOnObject(g14,g20)
    c: PointOnObject(g15,g20)
    c: PointOnObject(g16,g20)
    c: PointOnObject(g17,g20)
    c: PointOnObject(g18,g20)
    c: PointOnObject(g19,g20)
    c: Coincident(g21,g22)
    c: Coincident(g22,g23)
    c: Coincident(g23,g24)
    c: Coincident(g24,g25)
    c: Coincident(g25,g26)
    c: Coincident(g26,g21)
    c: Equal(g21, g22-g26) x5
    c: PointOnObject(g21,g27)
    c: PointOnObject(g22,g27)
    c: PointOnObject(g23,g27)
    c: PointOnObject(g24,g27)
    c: PointOnObject(g25,g27)
    c: PointOnObject(g26,g27)
    c: Equal(g20,g6)
    c: Equal(g6,g13)
    c: Equal(g13,g27)
    c: Coincident(g6,g-3)
    c: Coincident(g13,g-4)
    c: Coincident(g20,g-6)
    c: Coincident(g27,g-5)
    c: Vertical(g15)
    c: Vertical(g1)
    c: Vertical(g12)
    c: Vertical(g26)
    c: Distance(g23,g25) = 5.7
FEATURE [PartDesign::Pocket] Pocket049  label="Nutholes Covers003"
  BaseFeature = -> Pocket045
  Length = 9
  Length2 = 100
  Profile = -> Sketch108
  Type = 0
FEATURE [PartDesign::Fillet] Fillet017  label="Smooth Baseplate Corners006"
  Base = -> Pocket049 [Edge74,Edge7,Edge4,Edge1]
  BaseFeature = -> Pocket049
  Radius = 0.4
FEATURE [PartDesign::Fillet] Fillet019  label="Smooth Nutholes Front and Rear003"
  Base = -> Fillet017 [Edge104,Edge98,Edge111,Edge116,Edge101,Edge95,Edge109,Edge114,Edge105,Edge99,Edge117,Edge112,Edge115,Edge110,Edge96,Edge102]
  BaseFeature = -> Fillet017
  Radius = 0.2
FEATURE [PartDesign::Body] Body025  label="Bottom_Shoulder001"
  Group = -> [Sketch076,Pad1037,Sketch072,Pocket038,Sketch095,Pocket044,Sketch107,Pocket035,Sketch093,Pocket045,Sketch108,Pocket049,Fillet017,Fillet019]
  Origin = -> Origin038
  Placement = pos=(0,-55,0) rot=(0,0,1;0rad)
  Tip = -> Fillet019
FEATURE [Sketcher::SketchObject] Sketch079
  MapMode = 5
  Support = -> [XY_Plane949]
  sketch-geometry (8):
    g0: LineSegment StartX=0 StartY=3.17543 StartZ=0 EndX=-2.75 EndY=1.58771 EndZ=0
    g1: LineSegment StartX=-2.75 StartY=1.58771 StartZ=0 EndX=-2.75 EndY=-1.58771 EndZ=0
    g2: LineSegment StartX=-2.75 StartY=-1.58771 StartZ=0 EndX=0 EndY=-3.17543 EndZ=0
    g3: LineSegment StartX=0 StartY=-3.17543 StartZ=0 EndX=2.75 EndY=-1.58771 EndZ=0
    g4: LineSegment StartX=2.75 StartY=-1.58771 StartZ=0 EndX=2.75 EndY=1.58771 EndZ=0
    g5: LineSegment StartX=2.75 StartY=1.58771 StartZ=0 EndX=0 EndY=3.17543 EndZ=0
    g6: Circle [constr] CenterX=0 CenterY=0 CenterZ=0 NormalX=0 NormalY=0 NormalZ=1 AngleXU=0 Radius=3.17543
    g7: Circle CenterX=0 CenterY=0 CenterZ=0 NormalX=0 NormalY=0 NormalZ=1 AngleXU=0 Radius=1.5
  constraints (18):
    c: Coincident(g0,g1)
    c: Coincident(g1,g2)
    c: Coincident(g2,g3)
    c: Coincident(g3,g4)
    c: Coincident(g4,g5)
    c: Coincident(g5,g0)
    c: Equal(g0, g1-g5) x5
    c: PointOnObject(g0,g6)
    c: PointOnObject(g1,g6)
    c: PointOnObject(g2,g6)
    c: PointOnObject(g3,g6)
    c: PointOnObject(g4,g6)
    c: PointOnObject(g5,g6)
    c: Coincident(g6,g-1)
    c: PointOnObject(g5,g-2)
    c: DistanceX(g0,g4) = 5.5
    c: Coincident(g7,g-1)
    c: Radius(g7) = 1.5
FEATURE [PartDesign::Pad] Pad1036  label="M3 Nut Primitive207"
  Length = 1.2
  Length2 = 1.2
  Profile = -> Sketch079
  Type = 4
FEATURE [Sketcher::SketchObject] Sketch081
  ExternalGeometry = -> [Pad1036]
  MapMode = 5
  Placement = pos=(0,0,0) rot=(0.57735,0.57735,0.57735;2.0944rad)
  Support = -> [YZ_Plane940]
  sketch-geometry (6):
    g0: LineSegment StartX=-2.67543 StartY=1.2 StartZ=0 EndX=-3.67543 EndY=1.2 EndZ=0
    g1: LineSegment StartX=-3.67543 StartY=1.2 StartZ=0 EndX=-3.67543 EndY=-1.2 EndZ=0
    g2: LineSegment StartX=-3.67543 StartY=-1.2 StartZ=0 EndX=-2.67543 EndY=-1.2 EndZ=0
    g3: LineSegment StartX=-2.67543 StartY=-1.2 StartZ=0 EndX=-3.17543 EndY=-1 EndZ=0
    g4: LineSegment StartX=-3.17543 StartY=-1 StartZ=0 EndX=-3.17543 EndY=1 EndZ=0
    g5: LineSegment StartX=-3.17543 StartY=1 StartZ=0 EndX=-2.67543 EndY=1.2 EndZ=0
  constraints (15):
    c: Horizontal(g0)
    c: Coincident(g0,g1)
    c: Coincident(g1,g2)
    c: Coincident(g2,g3)
    c: Coincident(g3,g4)
    c: Coincident(g4,g5)
    c: Coincident(g5,g0)
    c: Symmetric(g4,g3,g-1)
    c: Symmetric(g0,g2,g-1)
    c: Symmetric(g1,g0,g-1)
    c: DistanceX(g0,g4) = 0.5
    c: DistanceY(g3,g4) = 2
    c: DistanceY(g1,g0) = 2.4
    c: PointOnObject(g3,g-3)
    c: DistanceX(g4,g0) = 0.5
FEATURE [PartDesign::Groove] Groove218  label="M3 Nut Smooth210"
  Angle = 360
  Axis = (-2e-16,3e-16,1)
  Base = (0,0,0)
  BaseFeature = -> Pad1036
  Profile = -> Sketch081
  ReferenceAxis = -> Sketch081 [V_Axis]
  Reversed = true
FEATURE [PartDesign::Chamfer] Chamfer512  label="M3 Nut Smooth Hole208"
  Base = -> Groove218 [Edge24,Edge23]
  BaseFeature = -> Groove218
  Size = 0.2
FEATURE [PartDesign::Body] Body671  label="M3 Nut112"
  Group = -> [Sketch079,Pad1036,Sketch081,Groove218,Chamfer512]
  Origin = -> Origin041
  Placement = pos=(-5,-35.75,6) rot=(1,0,0;1.5708rad)
  Tip = -> Chamfer512
FEATURE [App::Part] Part009  label="Bototm Shoudler001"
  Group = -> [Body025,Body671,Body023]
  Origin = -> Origin948
  Placement = pos=(0,26.2,0) rot=(0,0,1;0rad)
FEATURE [Sketcher::SketchObject] Sketch073
  MapMode = 5
  Placement = pos=(0,0,12) rot=(0,0,1;0rad)
  Support = -> [Pocket047]
  sketch-geometry (4):
    g0: Circle CenterX=-15 CenterY=5 CenterZ=0 NormalX=0 NormalY=0 NormalZ=1 AngleXU=0 Radius=1.6
    g1: Circle CenterX=15 CenterY=5 CenterZ=0 NormalX=0 NormalY=0 NormalZ=1 AngleXU=0 Radius=1.6
    g2: Circle CenterX=-15 CenterY=-5 CenterZ=0 NormalX=0 NormalY=0 NormalZ=1 AngleXU=0 Radius=1.6
    g3: Circle CenterX=15 CenterY=-5 CenterZ=0 NormalX=0 NormalY=0 NormalZ=1 AngleXU=0 Radius=1.6
  constraints (9):
    c: Equal(g0,g1)
    c: Equal(g1,g2)
    c: Equal(g2,g3)
    c: Symmetric(g3,g1,g-1)
    c: Symmetric(g0,g1,g-2)
    c: Symmetric(g2,g3,g-2)
    c: Radius(g1) = 1.6
    c: DistanceX(g0,g1) = 30
    c: DistanceY(g2,g0) = 10
FEATURE [PartDesign::Pocket] Pocket048  label="Screwholes Covers003"
  BaseFeature = -> Pocket047
  Length = 12
  Length2 = 100
  Profile = -> Sketch073
  Type = 0
FEATURE [Sketcher::SketchObject] Sketch086
  ExternalGeometry = -> [Pocket048]
  MapMode = 5
  Placement = pos=(0,0,12) rot=(0,0,1;0rad)
  Support = -> [Pocket048]
  sketch-geometry (28):
    g0: LineSegment StartX=-15 StartY=8.2909 StartZ=0 EndX=-17.85 EndY=6.64545 EndZ=0
    g1: LineSegment StartX=-17.85 StartY=6.64545 StartZ=0 EndX=-17.85 EndY=3.35455 EndZ=0
    g2: LineSegment StartX=-17.85 StartY=3.35455 StartZ=0 EndX=-15 EndY=1.7091 EndZ=0
    g3: LineSegment StartX=-15 StartY=1.7091 StartZ=0 EndX=-12.15 EndY=3.35455 EndZ=0
    g4: LineSegment StartX=-12.15 StartY=3.35455 StartZ=0 EndX=-12.15 EndY=6.64545 EndZ=0
    g5: LineSegment StartX=-12.15 StartY=6.64545 StartZ=0 EndX=-15 EndY=8.2909 EndZ=0
    g6: Circle [constr] CenterX=-15 CenterY=5 CenterZ=0 NormalX=0 NormalY=0 NormalZ=1 AngleXU=0 Radius=3.2909
    g7: LineSegment StartX=15 StartY=8.2909 StartZ=0 EndX=12.15 EndY=6.64545 EndZ=0
    g8: LineSegment StartX=12.15 StartY=6.64545 StartZ=0 EndX=12.15 EndY=3.35455 EndZ=0
    g9: LineSegment StartX=12.15 StartY=3.35455 StartZ=0 EndX=15 EndY=1.7091 EndZ=0
    g10: LineSegment StartX=15 StartY=1.7091 StartZ=0 EndX=17.85 EndY=3.35455 EndZ=0
    g11: LineSegment StartX=17.85 StartY=3.35455 StartZ=0 EndX=17.85 EndY=6.64545 EndZ=0
    g12: LineSegment StartX=17.85 StartY=6.64545 StartZ=0 EndX=15 EndY=8.2909 EndZ=0
    g13: Circle [constr] CenterX=15 CenterY=5 CenterZ=0 NormalX=0 NormalY=0 NormalZ=1 AngleXU=0 Radius=3.2909
    g14: LineSegment StartX=-15 StartY=-1.7091 StartZ=0 EndX=-17.85 EndY=-3.35455 EndZ=0
    g15: LineSegment StartX=-17.85 StartY=-3.35455 StartZ=0 EndX=-17.85 EndY=-6.64545 EndZ=0
    g16: LineSegment StartX=-17.85 StartY=-6.64545 StartZ=0 EndX=-15 EndY=-8.2909 EndZ=0
    g17: LineSegment StartX=-15 StartY=-8.2909 StartZ=0 EndX=-12.15 EndY=-6.64545 EndZ=0
    g18: LineSegment StartX=-12.15 StartY=-6.64545 StartZ=0 EndX=-12.15 EndY=-3.35455 EndZ=0
    g19: LineSegment StartX=-12.15 StartY=-3.35455 StartZ=0 EndX=-15 EndY=-1.7091 EndZ=0
    g20: Circle [constr] CenterX=-15 CenterY=-5 CenterZ=0 NormalX=0 NormalY=0 NormalZ=1 AngleXU=0 Radius=3.2909
    g21: LineSegment StartX=15 StartY=-1.7091 StartZ=0 EndX=12.15 EndY=-3.35455 EndZ=0
    g22: LineSegment StartX=12.15 StartY=-3.35455 StartZ=0 EndX=12.15 EndY=-6.64545 EndZ=0
    g23: LineSegment StartX=12.15 StartY=-6.64545 StartZ=0 EndX=15 EndY=-8.2909 EndZ=0
    g24: LineSegment StartX=15 StartY=-8.2909 StartZ=0 EndX=17.85 EndY=-6.64545 EndZ=0
    g25: LineSegment StartX=17.85 StartY=-6.64545 StartZ=0 EndX=17.85 EndY=-3.35455 EndZ=0
    g26: LineSegment StartX=17.85 StartY=-3.35455 StartZ=0 EndX=15 EndY=-1.7091 EndZ=0
    g27: Circle [constr] CenterX=15 CenterY=-5 CenterZ=0 NormalX=0 NormalY=0 NormalZ=1 AngleXU=0 Radius=3.2909
  constraints (64):
    c: Coincident(g0,g1)
    c: Coincident(g1,g2)
    c: Coincident(g2,g3)
    c: Coincident(g3,g4)
    c: Coincident(g4,g5)
    c: Coincident(g5,g0)
    c: Equal(g0, g1-g5) x5
    c: PointOnObject(g0,g6)
    c: PointOnObject(g1,g6)
    c: PointOnObject(g2,g6)
    c: PointOnObject(g3,g6)
    c: PointOnObject(g4,g6)
    c: PointOnObject(g5,g6)
    c: Coincident(g7,g8)
    c: Coincident(g8,g9)
    c: Coincident(g9,g10)
    c: Coincident(g10,g11)
    c: Coincident(g11,g12)
    c: Coincident(g12,g7)
    c: Equal(g7, g8-g12) x5
    c: PointOnObject(g7,g13)
    c: PointOnObject(g8,g13)
    c: PointOnObject(g9,g13)
    c: PointOnObject(g10,g13)
    c: PointOnObject(g11,g13)
    c: PointOnObject(g12,g13)
    c: Coincident(g14,g15)
    c: Coincident(g15,g16)
    c: Coincident(g16,g17)
    c: Coincident(g17,g18)
    c: Coincident(g18,g19)
    c: Coincident(g19,g14)
    c: Equal(g14, g15-g19) x5
    c: PointOnObject(g14,g20)
    c: PointOnObject(g15,g20)
    c: PointOnObject(g16,g20)
    c: PointOnObject(g17,g20)
    c: PointOnObject(g18,g20)
    c: PointOnObject(g19,g20)
    c: Coincident(g21,g22)
    c: Coincident(g22,g23)
    c: Coincident(g23,g24)
    c: Coincident(g24,g25)
    c: Coincident(g25,g26)
    c: Coincident(g26,g21)
    c: Equal(g21, g22-g26) x5
    c: PointOnObject(g21,g27)
    c: PointOnObject(g22,g27)
    c: PointOnObject(g23,g27)
    c: PointOnObject(g24,g27)
    c: PointOnObject(g25,g27)
    c: PointOnObject(g26,g27)
    c: Coincident(g13,g-5)
    c: Coincident(g27,g-6)
    c: Coincident(g6,g-3)
    c: Coincident(g20,g-4)
    c: Equal(g6,g20)
    c: Equal(g20,g13)
    c: Equal(g13,g27)
    c: Vertical(g1)
    c: Vertical(g15)
    c: Vertical(g8)
    c: Vertical(g22)
    c: Distance(g4,g0) = 5.7
FEATURE [PartDesign::Pocket] Pocket046  label="Nutholes Covers002"
  BaseFeature = -> Pocket048
  Length = 9
  Length2 = 100
  Profile = -> Sketch086
  Type = 0
FEATURE [PartDesign::Fillet] Fillet015  label="Smooth Baseplate Corners005"
  Base = -> Pocket046 [Edge7,Edge74,Edge4,Edge1]
  BaseFeature = -> Pocket046
  Radius = 0.4
FEATURE [PartDesign::Fillet] Fillet018  label="Smooth Nutholes Front and Rear002"
  Base = -> Fillet015 [Edge104,Edge120,Edge111,Edge98,Edge101,Edge118,Edge95,Edge109,Edge102,Edge119,Edge110,Edge96,Edge121,Edge112,Edge99,Edge105]
  BaseFeature = -> Fillet015
  Radius = 0.2
FEATURE [Sketcher::SketchObject] Sketch082
  MapMode = 5
  Placement = pos=(0,0,12) rot=(0,0,1;0rad)
  Support = -> [Fillet018]
  sketch-geometry (8):
    g0: LineSegment StartX=-2.5 StartY=12.5 StartZ=0 EndX=2.5 EndY=12.5 EndZ=0
    g1: LineSegment StartX=7.5 StartY=7.5 StartZ=0 EndX=7.5 EndY=-7.5 EndZ=0
    g2: LineSegment StartX=2.5 StartY=-12.5 StartZ=0 EndX=-2.5 EndY=-12.5 EndZ=0
    g3: LineSegment StartX=-7.5 StartY=-7.5 StartZ=0 EndX=-7.5 EndY=7.5 EndZ=0
    g4: ArcOfCircle CenterX=-2.5 CenterY=7.5 CenterZ=0 NormalX=0 NormalY=0 NormalZ=1 AngleXU=0 Radius=5 StartAngle=1.5708 EndAngle=3.14159
    g5: ArcOfCircle CenterX=2.5 CenterY=7.5 CenterZ=0 NormalX=0 NormalY=0 NormalZ=1 AngleXU=0 Radius=5 StartAngle=1e-16 EndAngle=1.5708
    g6: ArcOfCircle CenterX=2.5 CenterY=-7.5 CenterZ=0 NormalX=0 NormalY=0 NormalZ=1 AngleXU=0 Radius=5 StartAngle=4.71239 EndAngle=6.28319
    g7: ArcOfCircle CenterX=-2.5 CenterY=-7.5 CenterZ=0 NormalX=0 NormalY=0 NormalZ=1 AngleXU=0 Radius=5 StartAngle=3.14159 EndAngle=4.71239
  constraints (18):
    c: Horizontal(g2)
    c: Vertical(g3)
    c: Tangent(g3,g4) = 1.5708
    c: Tangent(g0,g4) = 1.5708
    c: Tangent(g0,g5) = 1.5708
    c: Tangent(g1,g5) = 1.5708
    c: Tangent(g1,g6) = 1.5708
    c: Tangent(g2,g6) = 1.5708
    c: Tangent(g2,g7) = 1.5708
    c: Tangent(g3,g7) = 1.5708
    c: Equal(g5,g6)
    c: Equal(g6,g4)
    c: Equal(g4,g7)
    c: Symmetric(g1,g3,g-2)
    c: Symmetric(g0,g2,g-1)
    c: DistanceY(g2,g0) = 25
    c: DistanceX(g3,g1) = 15
    c: Radius(g7) = 5
FEATURE [PartDesign::Pocket] Pocket827  label="Accesshole009"
  BaseFeature = -> Fillet018
  Length = 12
  Length2 = 100
  Profile = -> Sketch082
  Type = 0
FEATURE [PartDesign::Body] Body028  label="Top_Shoulder001"
  Group = -> [Sketch105,Pad1039,Sketch077,Pocket826,Sketch071,Pocket034,Sketch074,Pocket047,Sketch073,Pocket048,Sketch086,Pocket046,Fillet015,Fillet018,Sketch082,Pocket827]
  Origin = -> Origin037
  Placement = pos=(0,-130,60) rot=(0,0,1;0rad)
  Tip = -> Pocket827
FEATURE [App::Part] Part007  label="Top SHoulder001"
  Group = -> [Body028,Body029,Body670]
  Origin = -> Origin033
  Placement = pos=(-1.62e-14,101.25,130.25) rot=(0,1,0;3.14159rad)
FEATURE [Sketcher::SketchObject] Sketch2382
  MapMode = 5
  Support = -> [XY_Plane968]
  sketch-geometry (8):
    g0: LineSegment StartX=0 StartY=3.17543 StartZ=0 EndX=-2.75 EndY=1.58771 EndZ=0
    g1: LineSegment StartX=-2.75 StartY=1.58771 StartZ=0 EndX=-2.75 EndY=-1.58771 EndZ=0
    g2: LineSegment StartX=-2.75 StartY=-1.58771 StartZ=0 EndX=0 EndY=-3.17543 EndZ=0
    g3: LineSegment StartX=0 StartY=-3.17543 StartZ=0 EndX=2.75 EndY=-1.58771 EndZ=0
    g4: LineSegment StartX=2.75 StartY=-1.58771 StartZ=0 EndX=2.75 EndY=1.58771 EndZ=0
    g5: LineSegment StartX=2.75 StartY=1.58771 StartZ=0 EndX=0 EndY=3.17543 EndZ=0
    g6: Circle [constr] CenterX=0 CenterY=0 CenterZ=0 NormalX=0 NormalY=0 NormalZ=1 AngleXU=0 Radius=3.17543
    g7: Circle CenterX=0 CenterY=0 CenterZ=0 NormalX=0 NormalY=0 NormalZ=1 AngleXU=0 Radius=1.5
  constraints (18):
    c: Coincident(g0,g1)
    c: Coincident(g1,g2)
    c: Coincident(g2,g3)
    c: Coincident(g3,g4)
    c: Coincident(g4,g5)
    c: Coincident(g5,g0)
    c: Equal(g0, g1-g5) x5
    c: PointOnObject(g0,g6)
    c: PointOnObject(g1,g6)
    c: PointOnObject(g2,g6)
    c: PointOnObject(g3,g6)
    c: PointOnObject(g4,g6)
    c: PointOnObject(g5,g6)
    c: Coincident(g6,g-1)
    c: PointOnObject(g5,g-2)
    c: DistanceX(g0,g4) = 5.5
    c: Coincident(g7,g-1)
    c: Radius(g7) = 1.5
FEATURE [PartDesign::Pad] Pad1053  label="M3 Nut Primitive212"
  Length = 1.2
  Length2 = 1.2
  Profile = -> Sketch2382
  Type = 4
FEATURE [Sketcher::SketchObject] Sketch009
  MapMode = 5
  Support = -> [XY_Plane005]
  sketch-geometry (8):
    g0: LineSegment StartX=0 StartY=3.17543 StartZ=0 EndX=-2.75 EndY=1.58771 EndZ=0
    g1: LineSegment StartX=-2.75 StartY=1.58771 StartZ=0 EndX=-2.75 EndY=-1.58771 EndZ=0
    g2: LineSegment StartX=-2.75 StartY=-1.58771 StartZ=0 EndX=0 EndY=-3.17543 EndZ=0
    g3: LineSegment StartX=0 StartY=-3.17543 StartZ=0 EndX=2.75 EndY=-1.58771 EndZ=0
    g4: LineSegment StartX=2.75 StartY=-1.58771 StartZ=0 EndX=2.75 EndY=1.58771 EndZ=0
    g5: LineSegment StartX=2.75 StartY=1.58771 StartZ=0 EndX=0 EndY=3.17543 EndZ=0
    g6: Circle [constr] CenterX=0 CenterY=0 CenterZ=0 NormalX=0 NormalY=0 NormalZ=1 AngleXU=0 Radius=3.17543
    g7: Circle CenterX=0 CenterY=0 CenterZ=0 NormalX=0 NormalY=0 NormalZ=1 AngleXU=0 Radius=1.5
  constraints (18):
    c: Coincident(g0,g1)
    c: Coincident(g1,g2)
    c: Coincident(g2,g3)
    c: Coincident(g3,g4)
    c: Coincident(g4,g5)
    c: Coincident(g5,g0)
    c: Equal(g0, g1-g5) x5
    c: PointOnObject(g0,g6)
    c: PointOnObject(g1,g6)
    c: PointOnObject(g2,g6)
    c: PointOnObject(g3,g6)
    c: PointOnObject(g4,g6)
    c: PointOnObject(g5,g6)
    c: Coincident(g6,g-1)
    c: PointOnObject(g5,g-2)
    c: DistanceX(g0,g4) = 5.5
    c: Coincident(g7,g-1)
    c: Radius(g7) = 1.5
FEATURE [PartDesign::Pad] Pad1055  label="M3 Nut Primitive002"
  Length = 1.2
  Length2 = 1.2
  Profile = -> Sketch009
  Type = 4
FEATURE [Sketcher::SketchObject] Sketch010
  ExternalGeometry = -> [Pad1055]
  MapMode = 5
  Placement = pos=(0,0,0) rot=(0.57735,0.57735,0.57735;2.0944rad)
  Support = -> [YZ_Plane005]
  sketch-geometry (6):
    g0: LineSegment StartX=-2.67543 StartY=1.2 StartZ=0 EndX=-3.67543 EndY=1.2 EndZ=0
    g1: LineSegment StartX=-3.67543 StartY=1.2 StartZ=0 EndX=-3.67543 EndY=-1.2 EndZ=0
    g2: LineSegment StartX=-3.67543 StartY=-1.2 StartZ=0 EndX=-2.67543 EndY=-1.2 EndZ=0
    g3: LineSegment StartX=-2.67543 StartY=-1.2 StartZ=0 EndX=-3.17543 EndY=-1 EndZ=0
    g4: LineSegment StartX=-3.17543 StartY=-1 StartZ=0 EndX=-3.17543 EndY=1 EndZ=0
    g5: LineSegment StartX=-3.17543 StartY=1 StartZ=0 EndX=-2.67543 EndY=1.2 EndZ=0
  constraints (15):
    c: Horizontal(g0)
    c: Coincident(g0,g1)
    c: Coincident(g1,g2)
    c: Coincident(g2,g3)
    c: Coincident(g3,g4)
    c: Coincident(g4,g5)
    c: Coincident(g5,g0)
    c: Symmetric(g4,g3,g-1)
    c: Symmetric(g0,g2,g-1)
    c: Symmetric(g1,g0,g-1)
    c: DistanceX(g0,g4) = 0.5
    c: DistanceY(g3,g4) = 2
    c: DistanceY(g1,g0) = 2.4
    c: PointOnObject(g3,g-3)
    c: DistanceX(g4,g0) = 0.5
FEATURE [PartDesign::Groove] Groove002  label="M3 Nut Smooth002"
  Angle = 360
  Axis = (-2e-16,3e-16,1)
  Base = (0,0,0)
  BaseFeature = -> Pad1055
  Profile = -> Sketch010
  ReferenceAxis = -> Sketch010 [V_Axis]
  Reversed = true
FEATURE [PartDesign::Chamfer] Chamfer507  label="M3 Nut Smooth Hole002"
  Base = -> Groove002 [Edge24,Edge23]
  BaseFeature = -> Groove002
  Size = 0.2
FEATURE [PartDesign::Body] Body678  label="M3 Nut115"
  Group = -> [Sketch009,Pad1055,Sketch010,Groove002,Chamfer507]
  Origin = -> Origin005
  Placement = pos=(7.5,70.5,1.6e-14) rot=(1,0,0;1.5708rad)
  Tip = -> Chamfer507
FEATURE [Sketcher::SketchObject] Sketch2383
  ExternalGeometry = -> [Pad1053]
  MapMode = 5
  Placement = pos=(0,0,0) rot=(0.57735,0.57735,0.57735;2.0944rad)
  Support = -> [YZ_Plane961]
  sketch-geometry (6):
    g0: LineSegment StartX=-2.67543 StartY=1.2 StartZ=0 EndX=-3.67543 EndY=1.2 EndZ=0
    g1: LineSegment StartX=-3.67543 StartY=1.2 StartZ=0 EndX=-3.67543 EndY=-1.2 EndZ=0
    g2: LineSegment StartX=-3.67543 StartY=-1.2 StartZ=0 EndX=-2.67543 EndY=-1.2 EndZ=0
    g3: LineSegment StartX=-2.67543 StartY=-1.2 StartZ=0 EndX=-3.17543 EndY=-1 EndZ=0
    g4: LineSegment StartX=-3.17543 StartY=-1 StartZ=0 EndX=-3.17543 EndY=1 EndZ=0
    g5: LineSegment StartX=-3.17543 StartY=1 StartZ=0 EndX=-2.67543 EndY=1.2 EndZ=0
  constraints (15):
    c: Horizontal(g0)
    c: Coincident(g0,g1)
    c: Coincident(g1,g2)
    c: Coincident(g2,g3)
    c: Coincident(g3,g4)
    c: Coincident(g4,g5)
    c: Coincident(g5,g0)
    c: Symmetric(g4,g3,g-1)
    c: Symmetric(g0,g2,g-1)
    c: Symmetric(g1,g0,g-1)
    c: DistanceX(g0,g4) = 0.5
    c: DistanceY(g3,g4) = 2
    c: DistanceY(g1,g0) = 2.4
    c: PointOnObject(g3,g-3)
    c: DistanceX(g4,g0) = 0.5
FEATURE [PartDesign::Groove] Groove220  label="M3 Nut Smooth212"
  Angle = 360
  Axis = (-2e-16,3e-16,1)
  Base = (0,0,0)
  BaseFeature = -> Pad1053
  Profile = -> Sketch2383
  ReferenceAxis = -> Sketch2383 [V_Axis]
  Reversed = true
FEATURE [PartDesign::Chamfer] Chamfer500  label="M3 Nut Smooth Hole203"
  Base = -> Groove220 [Edge24,Edge23]
  BaseFeature = -> Groove220
  Size = 0.2
FEATURE [PartDesign::Body] Body672  label="M3 Nut113"
  Group = -> [Sketch2382,Pad1053,Sketch2383,Groove220,Chamfer500]
  Origin = -> Origin954
  Placement = pos=(-7.5,-70.5,-1.6e-14) rot=(1,0,0;1.5708rad)
  Tip = -> Chamfer500
FEATURE [Sketcher::SketchObject] Sketch078
  MapMode = 5
  Placement = pos=(0,0,5) rot=(0,0,1;0rad)
  Support = -> [Pad1034]
  sketch-geometry (8):
    g0: LineSegment StartX=-10 StartY=58 StartZ=0 EndX=10 EndY=58 EndZ=0
    g1: LineSegment StartX=20 StartY=48 StartZ=0 EndX=20 EndY=22 EndZ=0
    g2: LineSegment StartX=10 StartY=12 StartZ=0 EndX=-10 EndY=12 EndZ=0
    g3: LineSegment StartX=-20 StartY=22 StartZ=0 EndX=-20 EndY=48 EndZ=0
    g4: ArcOfCircle CenterX=-10 CenterY=48 CenterZ=0 NormalX=0 NormalY=0 NormalZ=1 AngleXU=0 Radius=10 StartAngle=1.5708 EndAngle=3.14159
    g5: ArcOfCircle CenterX=10 CenterY=48 CenterZ=0 NormalX=0 NormalY=0 NormalZ=1 AngleXU=0 Radius=10 StartAngle=2e-16 EndAngle=1.5708
    g6: ArcOfCircle CenterX=10 CenterY=22 CenterZ=0 NormalX=0 NormalY=0 NormalZ=1 AngleXU=0 Radius=10 StartAngle=4.71239 EndAngle=6.28319
    g7: ArcOfCircle CenterX=-10 CenterY=22 CenterZ=0 NormalX=0 NormalY=0 NormalZ=1 AngleXU=0 Radius=10 StartAngle=3.14159 EndAngle=4.71239
  constraints (19):
    c: Horizontal(g0)
    c: Vertical(g1)
    c: Vertical(g3)
    c: Tangent(g3,g4) = 1.5708
    c: Tangent(g0,g4) = 1.5708
    c: Tangent(g0,g5) = 1.5708
    c: Tangent(g1,g5) = 1.5708
    c: Tangent(g1,g6) = 1.5708
    c: Tangent(g2,g6) = 1.5708
    c: Tangent(g2,g7) = 1.5708
    c: Tangent(g3,g7) = 1.5708
    c: Equal(g5,g4)
    c: Equal(g4,g7)
    c: Equal(g7,g6)
    c: Symmetric(g2,g2,g-2)
    c: DistanceX(g3,g1) = 40
    c: DistanceY(g-1,g2) = 12
    c: DistanceY(g2,g0) = 46
    c: Radius(g5) = 10
FEATURE [PartDesign::Pocket] Pocket031  label="Accesshole008"
  BaseFeature = -> Pad1034
  Length = 5
  Length2 = 100
  Profile = -> Sketch078
  Type = 0
FEATURE [Sketcher::SketchObject] Sketch092
  MapMode = 5
  Placement = pos=(0,0,5) rot=(0,0,1;0rad)
  Support = -> [Pocket031]
  sketch-geometry (8):
    g0: Circle CenterX=-51.75 CenterY=45 CenterZ=0 NormalX=0 NormalY=0 NormalZ=1 AngleXU=0 Radius=1.6
    g1: Circle CenterX=-51.75 CenterY=30 CenterZ=0 NormalX=0 NormalY=0 NormalZ=1 AngleXU=0 Radius=1.6
    g2: Circle CenterX=-5 CenterY=6 CenterZ=0 NormalX=0 NormalY=0 NormalZ=1 AngleXU=0 Radius=1.6
    g3: Circle CenterX=5 CenterY=6 CenterZ=0 NormalX=0 NormalY=0 NormalZ=1 AngleXU=0 Radius=1.6
    g4: Circle CenterX=15 CenterY=64 CenterZ=0 NormalX=0 NormalY=0 NormalZ=1 AngleXU=0 Radius=1.6
    g5: Circle CenterX=-15 CenterY=64 CenterZ=0 NormalX=0 NormalY=0 NormalZ=1 AngleXU=0 Radius=1.6
    g6: Circle CenterX=51.75 CenterY=45 CenterZ=0 NormalX=0 NormalY=0 NormalZ=1 AngleXU=0 Radius=1.6
    g7: Circle CenterX=51.75 CenterY=30 CenterZ=0 NormalX=0 NormalY=0 NormalZ=1 AngleXU=0 Radius=1.6
  constraints (20):
    c: Equal(g1,g0)
    c: Equal(g1,g5)
    c: Equal(g1,g4)
    c: Equal(g1,g6)
    c: Equal(g1,g7)
    c: Equal(g1,g3)
    c: Equal(g1,g2)
    c: Symmetric(g2,g3,g-2)
    c: Symmetric(g5,g4,g-2)
    c: Symmetric(g0,g6,g-2)
    c: Symmetric(g1,g7,g-2)
    c: Vertical(g7,g6)
    c: DistanceX(g5,g4) = 30
    c: DistanceX(g2,g3) = 10
    c: DistanceY(g-1,g1) = 30
    c: DistanceY(g1,g0) = 15
    c: DistanceX(g1,g-1) = 51.75
    c: DistanceY(g-1,g2) = 6
    c: Radius(g6) = 1.6
    c: DistanceY(g-1,g4) = 64
FEATURE [PartDesign::Pocket] Pocket824  label="Screwholes011"
  BaseFeature = -> Pocket031
  Length = 5
  Length2 = 100
  Profile = -> Sketch092
  Type = 0
FEATURE [Sketcher::SketchObject] Sketch069
  ExternalGeometry = -> [Pocket824]
  MapMode = 5
  Placement = pos=(0,0,5) rot=(0,0,1;0rad)
  Support = -> [Pocket824]
  sketch-geometry (16):
    g0: ArcOfCircle CenterX=51.75 CenterY=45 CenterZ=0 NormalX=0 NormalY=0 NormalZ=1 AngleXU=0 Radius=3 StartAngle=1.5708 EndAngle=4.71239
    g1: ArcOfCircle CenterX=61.75 CenterY=45 CenterZ=0 NormalX=0 NormalY=0 NormalZ=1 AngleXU=0 Radius=3 StartAngle=4.71239 EndAngle=7.85398
    g2: LineSegment StartX=51.75 StartY=42 StartZ=0 EndX=61.75 EndY=42 EndZ=0
    g3: LineSegment StartX=51.75 StartY=48 StartZ=0 EndX=61.75 EndY=48 EndZ=0
    g4: ArcOfCircle CenterX=51.75 CenterY=30 CenterZ=0 NormalX=0 NormalY=0 NormalZ=1 AngleXU=0 Radius=3 StartAngle=1.5708 EndAngle=4.71239
    g5: ArcOfCircle CenterX=61.75 CenterY=30 CenterZ=0 NormalX=0 NormalY=0 NormalZ=1 AngleXU=0 Radius=3 StartAngle=4.71239 EndAngle=7.85398
    g6: LineSegment StartX=51.75 StartY=27 StartZ=0 EndX=61.75 EndY=27 EndZ=0
    g7: LineSegment StartX=51.75 StartY=33 StartZ=0 EndX=61.75 EndY=33 EndZ=0
    g8: ArcOfCircle CenterX=-51.75 CenterY=45 CenterZ=0 NormalX=0 NormalY=0 NormalZ=1 AngleXU=0 Radius=3 StartAngle=4.71239 EndAngle=7.85398
    g9: ArcOfCircle CenterX=-61.75 CenterY=45 CenterZ=0 NormalX=0 NormalY=0 NormalZ=1 AngleXU=0 Radius=3 StartAngle=1.5708 EndAngle=4.71239
    g10: LineSegment StartX=-51.75 StartY=48 StartZ=0 EndX=-61.75 EndY=48 EndZ=0
    g11: LineSegment StartX=-51.75 StartY=42 StartZ=0 EndX=-61.75 EndY=42 EndZ=0
    g12: ArcOfCircle CenterX=-51.75 CenterY=30 CenterZ=0 NormalX=0 NormalY=0 NormalZ=1 AngleXU=0 Radius=3 StartAngle=4.71239 EndAngle=7.85398
    g13: ArcOfCircle CenterX=-61.75 CenterY=30 CenterZ=0 NormalX=0 NormalY=0 NormalZ=1 AngleXU=0 Radius=3 StartAngle=1.5708 EndAngle=4.71239
    g14: LineSegment StartX=-51.75 StartY=33 StartZ=0 EndX=-61.75 EndY=33 EndZ=0
    g15: LineSegment StartX=-51.75 StartY=27 StartZ=0 EndX=-61.75 EndY=27 EndZ=0
  constraints (36):
    c: Tangent(g0,g3) = 1.5708
    c: Tangent(g0,g2) = -1.5708
    c: Tangent(g2,g1) = -1.5708
    c: Tangent(g3,g1) = 1.5708
    c: Horizontal(g2)
    c: Equal(g0,g1)
    c: Coincident(g0,g-5)
    c: Tangent(g4,g7) = 1.5708
    c: Tangent(g4,g6) = -1.5708
    c: Tangent(g6,g5) = -1.5708
    c: Tangent(g7,g5) = 1.5708
    c: Horizontal(g6)
    c: Equal(g4,g5)
    c: Coincident(g4,g-6)
    c: Tangent(g8,g11) = 1.5708
    c: Tangent(g8,g10) = -1.5708
    c: Tangent(g10,g9) = -1.5708
    c: Tangent(g11,g9) = 1.5708
    c: Horizontal(g10)
    c: Equal(g8,g9)
    c: Coincident(g8,g-3)
    c: Tangent(g12,g15) = 1.5708
    c: Tangent(g12,g14) = -1.5708
    c: Tangent(g14,g13) = -1.5708
    c: Tangent(g15,g13) = 1.5708
    c: Horizontal(g14)
    c: Equal(g12,g13)
    c: Coincident(g12,g-4)
    c: Equal(g8,g12)
    c: Equal(g12,g0)
    c: Equal(g0,g4)
    c: Equal(g3,g10)
    c: Equal(g10,g14)
    c: Equal(g14,g7)
    c: Radius(g1) = 3
    c: DistanceX(g3,g3) = 10
FEATURE [PartDesign::Pocket] Pocket040  label="Screwheads Top001"
  BaseFeature = -> Pocket824
  Length = 3
  Length2 = 100
  Profile = -> Sketch069
  Type = 0
FEATURE [PartDesign::Fillet] Fillet016  label="Screwheads Top Fillet001"
  Base = -> Pocket040 [Edge87,Edge89,Edge90,Edge92,Edge4,Edge6,Edge8,Edge10]
  BaseFeature = -> Pocket040
  Radius = 1
FEATURE [Sketcher::SketchObject] Sketch106
  MapMode = 5
  Placement = pos=(0,0,0) rot=(1,0,0;3.14159rad)
  Support = -> [Fillet016]
  sketch-geometry (4):
    g0: Circle CenterX=-5 CenterY=-6 CenterZ=0 NormalX=0 NormalY=0 NormalZ=1 AngleXU=0 Radius=2.85
    g1: Circle CenterX=5 CenterY=-6 CenterZ=0 NormalX=0 NormalY=0 NormalZ=1 AngleXU=0 Radius=2.85
    g2: Circle CenterX=-15 CenterY=-64 CenterZ=0 NormalX=0 NormalY=0 NormalZ=1 AngleXU=0 Radius=2.85
    g3: Circle CenterX=15 CenterY=-64 CenterZ=0 NormalX=0 NormalY=0 NormalZ=1 AngleXU=0 Radius=2.85
  constraints (10):
    c: Symmetric(g0,g1,g-2)
    c: Symmetric(g2,g3,g-2)
    c: Equal(g0,g1)
    c: Equal(g1,g2)
    c: Equal(g2,g3)
    c: Radius(g1) = 2.85
    c: DistanceX(g0,g1) = 10
    c: DistanceX(g2,g3) = 30
    c: DistanceY(g1,g-1) = 6
    c: DistanceY(g2,g-1) = 64
FEATURE [PartDesign::Pocket] Pocket822  label="Screwheads Bottom001"
  BaseFeature = -> Fillet016
  Length = 2
  Length2 = 100
  Profile = -> Sketch106
  Type = 0
FEATURE [PartDesign::Chamfer] Chamfer511  label="Screwheads Bottom Chamfer005"
  Base = -> Pocket822 [Edge136,Edge138,Edge148,Edge150]
  BaseFeature = -> Pocket822
  Size = 1.2
FEATURE [Sketcher::SketchObject] Sketch104
  MapMode = 5
  Placement = pos=(0,0,5) rot=(0,0,1;0rad)
  Support = -> [Chamfer511]
  sketch-geometry (2):
    g0: Circle CenterX=-39 CenterY=44 CenterZ=0 NormalX=0 NormalY=0 NormalZ=1 AngleXU=0 Radius=8.15
    g1: Circle CenterX=39 CenterY=44 CenterZ=0 NormalX=0 NormalY=0 NormalZ=1 AngleXU=0 Radius=8.15
  constraints (5):
    c: Symmetric(g0,g1,g-2)
    c: DistanceX(g0,g1) = 78
    c: DistanceY(g-1,g0) = 44
    c: Radius(g0) = 8.15
    c: Equal(g0,g1)
FEATURE [PartDesign::Pocket] Pocket825  label="Ball Bearing Flange005"
  BaseFeature = -> Chamfer511
  Length = 4
  Length2 = 100
  Profile = -> Sketch104
  Type = 0
FEATURE [Sketcher::SketchObject] Sketch075
  MapMode = 5
  Placement = pos=(0,0,1) rot=(0,0,1;0rad)
  Support = -> [Pocket825]
  sketch-geometry (2):
    g0: Circle CenterX=-39 CenterY=44 CenterZ=0 NormalX=0 NormalY=0 NormalZ=1 AngleXU=0 Radius=6.15
    g1: Circle CenterX=39 CenterY=44 CenterZ=0 NormalX=0 NormalY=0 NormalZ=1 AngleXU=0 Radius=6.15
  constraints (5):
    c: Symmetric(g1,g0,g-2)
    c: DistanceX(g0,g1) = 78
    c: DistanceY(g-1,g0) = 44
    c: Radius(g0) = 6.15
    c: Equal(g0,g1)
FEATURE [PartDesign::Pocket] Pocket823  label="Ball Bearing005"
  BaseFeature = -> Pocket825
  Length = 1
  Length2 = 100
  Profile = -> Sketch075
  Type = 0
FEATURE [PartDesign::Body] Body024  label="Inner_Shoulder001"
  Group = -> [Sketch103,Pad1034,Sketch078,Pocket031,Sketch092,Pocket824,Sketch069,Pocket040,Fillet016,Sketch106,Pocket822,Chamfer511,Sketch104,Pocket825,Sketch075,Pocket823]
  Origin = -> Origin945
  Placement = pos=(0,0,0) rot=(1,0,0;1.5708rad)
  Tip = -> Pocket823
FEATURE [App::Part] Part006  label="Front Inner SHoulder Assembly001"
  Group = -> [Body024,Part009,Part007,Part008]
  Origin = -> Origin950
  Placement = pos=(55,75.25,-37.5) rot=(0,0,1;3.14159rad)
FEATURE [Sketcher::SketchObject] Sketch2385
  MapMode = 5
  Support = -> [XY_Plane967]
  sketch-geometry (4):
    g0: LineSegment StartX=-12.5 StartY=75 StartZ=0 EndX=12.5 EndY=75 EndZ=0
    g1: LineSegment StartX=12.5 StartY=75 StartZ=0 EndX=12.5 EndY=-75 EndZ=0
    g2: LineSegment StartX=12.5 StartY=-75 StartZ=0 EndX=-12.5 EndY=-75 EndZ=0
    g3: LineSegment StartX=-12.5 StartY=-75 StartZ=0 EndX=-12.5 EndY=75 EndZ=0
  constraints (10):
    c: Coincident(g0,g1)
    c: Coincident(g1,g2)
    c: Coincident(g2,g3)
    c: Coincident(g3,g0)
    c: Horizontal(g2)
    c: Vertical(g3)
    c: Symmetric(g0,g0,g-2)
    c: Symmetric(g1,g0,g-1)
    c: DistanceX(g0,g0) = 25
    c: DistanceY(g1,g0) = 150
FEATURE [PartDesign::Pad] Pad1052  label="Baseplate046"
  Length = 6.5
  Length2 = 100
  Profile = -> Sketch2385
  Type = 0
FEATURE [Sketcher::SketchObject] Sketch2384
  MapMode = 5
  Placement = pos=(0,-75,0) rot=(1,0,0;1.5708rad)
  Support = -> [Pad1052]
  sketch-geometry (2):
    g0: Circle CenterX=-7.5 CenterY=3.25 CenterZ=0 NormalX=0 NormalY=0 NormalZ=1 AngleXU=0 Radius=1.6
    g1: Circle CenterX=7.5 CenterY=3.25 CenterZ=0 NormalX=0 NormalY=0 NormalZ=1 AngleXU=0 Radius=1.6
  constraints (5):
    c: Symmetric(g0,g1,g-2)
    c: DistanceY(g-1,g0) = 3.25
    c: Equal(g0,g1)
    c: Radius(g1) = 1.6
    c: DistanceX(g0,g1) = 15
FEATURE [PartDesign::Pocket] Pocket844  label="Screwholes Front"
  BaseFeature = -> Pad1052
  Length = 10
  Length2 = 100
  Profile = -> Sketch2384
  Type = 0
FEATURE [Sketcher::SketchObject] Sketch2381
  MapMode = 5
  Placement = pos=(0,75,0) rot=(0,0.707107,0.707107;3.14159rad)
  Support = -> [Pocket844]
  sketch-geometry (2):
    g0: Circle CenterX=-7.5 CenterY=3.25 CenterZ=0 NormalX=0 NormalY=0 NormalZ=1 AngleXU=0 Radius=1.6
    g1: Circle CenterX=7.5 CenterY=3.25 CenterZ=0 NormalX=0 NormalY=0 NormalZ=1 AngleXU=0 Radius=1.6
  constraints (5):
    c: Symmetric(g1,g0,g-2)
    c: Equal(g0,g1)
    c: DistanceY(g-1,g0) = 3.25
    c: Radius(g1) = 1.6
    c: DistanceX(g0,g1) = 15
FEATURE [PartDesign::Pocket] Pocket841  label="Screwholes Rear"
  BaseFeature = -> Pocket844
  Length = 10
  Length2 = 100
  Profile = -> Sketch2381
  Type = 0
FEATURE [Sketcher::SketchObject] Sketch2387
  MapMode = 5
  Placement = pos=(0,0,6.5) rot=(0,0,1;0rad)
  Support = -> [Pocket841]
  sketch-geometry (16):
    g0: LineSegment StartX=-10.4 StartY=72 StartZ=0 EndX=-4.6 EndY=72 EndZ=0
    g1: LineSegment StartX=-4.6 StartY=72 StartZ=0 EndX=-4.6 EndY=69 EndZ=0
    g2: LineSegment StartX=-4.6 StartY=69 StartZ=0 EndX=-10.4 EndY=69 EndZ=0
    g3: LineSegment StartX=-10.4 StartY=69 StartZ=0 EndX=-10.4 EndY=72 EndZ=0
    g4: LineSegment StartX=4.6 StartY=72 StartZ=0 EndX=10.4 EndY=72 EndZ=0
    g5: LineSegment StartX=10.4 StartY=72 StartZ=0 EndX=10.4 EndY=69 EndZ=0
    g6: LineSegment StartX=10.4 StartY=69 StartZ=0 EndX=4.6 EndY=69 EndZ=0
    g7: LineSegment StartX=4.6 StartY=69 StartZ=0 EndX=4.6 EndY=72 EndZ=0
    g8: LineSegment StartX=-10.4 StartY=-69 StartZ=0 EndX=-4.6 EndY=-69 EndZ=0
    g9: LineSegment StartX=-4.6 StartY=-69 StartZ=0 EndX=-4.6 EndY=-72 EndZ=0
    g10: LineSegment StartX=-4.6 StartY=-72 StartZ=0 EndX=-10.4 EndY=-72 EndZ=0
    g11: LineSegment StartX=-10.4 StartY=-72 StartZ=0 EndX=-10.4 EndY=-69 EndZ=0
    g12: LineSegment StartX=4.6 StartY=-69 StartZ=0 EndX=10.4 EndY=-69 EndZ=0
    g13: LineSegment StartX=10.4 StartY=-69 StartZ=0 EndX=10.4 EndY=-72 EndZ=0
    g14: LineSegment StartX=10.4 StartY=-72 StartZ=0 EndX=4.6 EndY=-72 EndZ=0
    g15: LineSegment StartX=4.6 StartY=-72 StartZ=0 EndX=4.6 EndY=-69 EndZ=0
  constraints (45):
    c: Coincident(g0,g1)
    c: Coincident(g1,g2)
    c: Coincident(g2,g3)
    c: Coincident(g3,g0)
    c: Horizontal(g0)
    c: Horizontal(g2)
    c: Vertical(g1)
    c: Vertical(g3)
    c: Coincident(g4,g5)
    c: Coincident(g5,g6)
    c: Coincident(g6,g7)
    c: Coincident(g7,g4)
    c: Horizontal(g4)
    c: Horizontal(g6)
    c: Vertical(g5)
    c: Vertical(g7)
    c: Coincident(g8,g9)
    c: Coincident(g9,g10)
    c: Coincident(g10,g11)
    c: Coincident(g11,g8)
    c: Horizontal(g8)
    c: Horizontal(g10)
    c: Vertical(g9)
    c: Vertical(g11)
    c: Coincident(g12,g13)
    c: Coincident(g13,g14)
    c: Coincident(g14,g15)
    c: Coincident(g15,g12)
    c: Horizontal(g12)
    c: Horizontal(g14)
    c: Vertical(g13)
    c: Vertical(g15)
    c: Symmetric(g9,g14,g-2)
    c: Symmetric(g0,g4,g-2)
    c: Equal(g3,g5)
    c: Equal(g5,g13)
    c: Equal(g13,g11)
    c: Equal(g10,g14)
    c: Equal(g14,g0)
    c: Equal(g0,g4)
    c: DistanceX(g4,g4) = 5.8
    c: DistanceY(g3,g3) = 3
    c: DistanceY(g-1,g4) = 72
    c: DistanceX(g0,g4) = 9.2
    c: Symmetric(g12,g5,g-1)
FEATURE [PartDesign::Pocket] Pocket842  label="Nutholes Front and Rear"
  BaseFeature = -> Pocket841
  Length = 6.5
  Length2 = 100
  Profile = -> Sketch2387
  Type = 0
FEATURE [PartDesign::Fillet] Fillet255  label="Smooth Baseplate Corners"
  Base = -> Pocket842 [Edge7,Edge46,Edge4,Edge1]
  BaseFeature = -> Pocket842
  Radius = 0.4
FEATURE [PartDesign::Fillet] Fillet001  label="Smooth Nuthole Corners"
  Base = -> Fillet255 [Edge77,Edge82,Edge71,Edge65,Edge72,Edge66,Edge78,Edge83,Edge84,Edge79,Edge68,Edge74,Edge75,Edge69,Edge80,Edge85]
  BaseFeature = -> Fillet255
  Radius = 0.2
FEATURE [Sketcher::SketchObject] Sketch2386
  MapMode = 5
  Placement = pos=(0,0,6.5) rot=(0,0,1;0rad)
  Support = -> [Fillet001]
  sketch-geometry (8):
    g0: LineSegment StartX=-10 StartY=-60 StartZ=0 EndX=-10 EndY=60 EndZ=0
    g1: LineSegment StartX=-10 StartY=60 StartZ=0 EndX=-4.5 EndY=60 EndZ=0
    g2: LineSegment StartX=-4.5 StartY=60 StartZ=0 EndX=-4.5 EndY=50 EndZ=0
    g3: LineSegment StartX=-4.5 StartY=50 StartZ=0 EndX=10 EndY=50 EndZ=0
    g4: LineSegment StartX=10 StartY=50 StartZ=0 EndX=10 EndY=-50 EndZ=0
    g5: LineSegment StartX=10 StartY=-50 StartZ=0 EndX=-4.5 EndY=-50 EndZ=0
    g6: LineSegment StartX=-4.5 StartY=-50 StartZ=0 EndX=-4.5 EndY=-60 EndZ=0
    g7: LineSegment StartX=-4.5 StartY=-60 StartZ=0 EndX=-10 EndY=-60 EndZ=0
  constraints (22):
    c: Coincident(g0,g1)
    c: Horizontal(g1)
    c: Coincident(g1,g2)
    c: Vertical(g2)
    c: Coincident(g2,g3)
    c: Horizontal(g3)
    c: Coincident(g3,g4)
    c: Coincident(g4,g5)
    c: Coincident(g5,g6)
    c: Vertical(g6)
    c: Coincident(g6,g7)
    c: Coincident(g7,g0)
    c: Equal(g2,g6)
    c: Equal(g3,g5)
    c: Symmetric(g2,g5,g-1)
    c: Symmetric(g3,g4,g-1)
    c: Symmetric(g0,g0,g-1)
    c: DistanceY(g0,g0) = 120
    c: DistanceX(g1,g1) = 5.5
    c: DistanceX(g1,g-1) = 4.5
    c: DistanceX(g-1,g3) = 10
    c: DistanceY(g2,g2) = 10
FEATURE [PartDesign::Pocket] Pocket843  label="Circuitboard Mount"
  BaseFeature = -> Fillet001
  Length = 5
  Length2 = 100
  Profile = -> Sketch2386
  Type = 0
FEATURE [PartDesign::Fillet] Fillet002  label="Smooth Circuitboard Mount Top Corners"
  Base = -> Pocket843 [Edge158,Edge160,Edge164,Edge162]
  BaseFeature = -> Pocket843
  Radius = 1
FEATURE [PartDesign::Fillet] Fillet003  label="Smooth Circuitboard Mount Bottom Corners"
  Base = -> Fillet002 [Edge54,Edge58,Edge66,Edge62]
  BaseFeature = -> Fillet002
  Radius = 0.2
FEATURE [PartDesign::Body] Body673  label="Chassis_Side"
  Group = -> [Sketch2385,Pad1052,Sketch2384,Pocket844,Sketch2381,Pocket841,Sketch2387,Pocket842,Fillet255,Fillet001,Sketch2386,Pocket843,Fillet002,Fillet003]
  Origin = -> Origin953
  Placement = pos=(0,0,0) rot=(0.707107,0,0.707107;3.14159rad)
  Tip = -> Fillet003
FEATURE [Sketcher::SketchObject] Sketch2388
  MapMode = 5
  Support = -> [XY_Plane004]
  sketch-geometry (8):
    g0: LineSegment StartX=0 StartY=3.17543 StartZ=0 EndX=-2.75 EndY=1.58771 EndZ=0
    g1: LineSegment StartX=-2.75 StartY=1.58771 StartZ=0 EndX=-2.75 EndY=-1.58771 EndZ=0
    g2: LineSegment StartX=-2.75 StartY=-1.58771 StartZ=0 EndX=0 EndY=-3.17543 EndZ=0
    g3: LineSegment StartX=0 StartY=-3.17543 StartZ=0 EndX=2.75 EndY=-1.58771 EndZ=0
    g4: LineSegment StartX=2.75 StartY=-1.58771 StartZ=0 EndX=2.75 EndY=1.58771 EndZ=0
    g5: LineSegment StartX=2.75 StartY=1.58771 StartZ=0 EndX=0 EndY=3.17543 EndZ=0
    g6: Circle [constr] CenterX=0 CenterY=0 CenterZ=0 NormalX=0 NormalY=0 NormalZ=1 AngleXU=0 Radius=3.17543
    g7: Circle CenterX=0 CenterY=0 CenterZ=0 NormalX=0 NormalY=0 NormalZ=1 AngleXU=0 Radius=1.5
  constraints (18):
    c: Coincident(g0,g1)
    c: Coincident(g1,g2)
    c: Coincident(g2,g3)
    c: Coincident(g3,g4)
    c: Coincident(g4,g5)
    c: Coincident(g5,g0)
    c: Equal(g0, g1-g5) x5
    c: PointOnObject(g0,g6)
    c: PointOnObject(g1,g6)
    c: PointOnObject(g2,g6)
    c: PointOnObject(g3,g6)
    c: PointOnObject(g4,g6)
    c: PointOnObject(g5,g6)
    c: Coincident(g6,g-1)
    c: PointOnObject(g5,g-2)
    c: DistanceX(g0,g4) = 5.5
    c: Coincident(g7,g-1)
    c: Radius(g7) = 1.5
FEATURE [PartDesign::Pad] Pad1054  label="M3 Nut Primitive001"
  Length = 1.2
  Length2 = 1.2
  Profile = -> Sketch2388
  Type = 4
FEATURE [Sketcher::SketchObject] Sketch008
  ExternalGeometry = -> [Pad1054]
  MapMode = 5
  Placement = pos=(0,0,0) rot=(0.57735,0.57735,0.57735;2.0944rad)
  Support = -> [YZ_Plane004]
  sketch-geometry (6):
    g0: LineSegment StartX=-2.67543 StartY=1.2 StartZ=0 EndX=-3.67543 EndY=1.2 EndZ=0
    g1: LineSegment StartX=-3.67543 StartY=1.2 StartZ=0 EndX=-3.67543 EndY=-1.2 EndZ=0
    g2: LineSegment StartX=-3.67543 StartY=-1.2 StartZ=0 EndX=-2.67543 EndY=-1.2 EndZ=0
    g3: LineSegment StartX=-2.67543 StartY=-1.2 StartZ=0 EndX=-3.17543 EndY=-1 EndZ=0
    g4: LineSegment StartX=-3.17543 StartY=-1 StartZ=0 EndX=-3.17543 EndY=1 EndZ=0
    g5: LineSegment StartX=-3.17543 StartY=1 StartZ=0 EndX=-2.67543 EndY=1.2 EndZ=0
  constraints (15):
    c: Horizontal(g0)
    c: Coincident(g0,g1)
    c: Coincident(g1,g2)
    c: Coincident(g2,g3)
    c: Coincident(g3,g4)
    c: Coincident(g4,g5)
    c: Coincident(g5,g0)
    c: Symmetric(g4,g3,g-1)
    c: Symmetric(g0,g2,g-1)
    c: Symmetric(g1,g0,g-1)
    c: DistanceX(g0,g4) = 0.5
    c: DistanceY(g3,g4) = 2
    c: DistanceY(g1,g0) = 2.4
    c: PointOnObject(g3,g-3)
    c: DistanceX(g4,g0) = 0.5
FEATURE [PartDesign::Groove] Groove001  label="M3 Nut Smooth001"
  Angle = 360
  Axis = (-2e-16,3e-16,1)
  Base = (0,0,0)
  BaseFeature = -> Pad1054
  Profile = -> Sketch008
  ReferenceAxis = -> Sketch008 [V_Axis]
  Reversed = true
FEATURE [PartDesign::Chamfer] Chamfer501  label="M3 Nut Smooth Hole001"
  Base = -> Groove001 [Edge24,Edge23]
  BaseFeature = -> Groove001
  Size = 0.2
FEATURE [PartDesign::Body] Body004  label="M3 Nut114"
  Group = -> [Sketch2388,Pad1054,Sketch008,Groove001,Chamfer501]
  Origin = -> Origin004
  Placement = pos=(7.5,-70.5,-1.6e-14) rot=(1,0,0;1.5708rad)
  Tip = -> Chamfer501
FEATURE [Sketcher::SketchObject] Sketch011
  MapMode = 5
  Support = -> [XY_Plane006]
  sketch-geometry (8):
    g0: LineSegment StartX=0 StartY=3.17543 StartZ=0 EndX=-2.75 EndY=1.58771 EndZ=0
    g1: LineSegment StartX=-2.75 StartY=1.58771 StartZ=0 EndX=-2.75 EndY=-1.58771 EndZ=0
    g2: LineSegment StartX=-2.75 StartY=-1.58771 StartZ=0 EndX=0 EndY=-3.17543 EndZ=0
    g3: LineSegment StartX=0 StartY=-3.17543 StartZ=0 EndX=2.75 EndY=-1.58771 EndZ=0
    g4: LineSegment StartX=2.75 StartY=-1.58771 StartZ=0 EndX=2.75 EndY=1.58771 EndZ=0
    g5: LineSegment StartX=2.75 StartY=1.58771 StartZ=0 EndX=0 EndY=3.17543 EndZ=0
    g6: Circle [constr] CenterX=0 CenterY=0 CenterZ=0 NormalX=0 NormalY=0 NormalZ=1 AngleXU=0 Radius=3.17543
    g7: Circle CenterX=0 CenterY=0 CenterZ=0 NormalX=0 NormalY=0 NormalZ=1 AngleXU=0 Radius=1.5
  constraints (18):
    c: Coincident(g0,g1)
    c: Coincident(g1,g2)
    c: Coincident(g2,g3)
    c: Coincident(g3,g4)
    c: Coincident(g4,g5)
    c: Coincident(g5,g0)
    c: Equal(g0, g1-g5) x5
    c: PointOnObject(g0,g6)
    c: PointOnObject(g1,g6)
    c: PointOnObject(g2,g6)
    c: PointOnObject(g3,g6)
    c: PointOnObject(g4,g6)
    c: PointOnObject(g5,g6)
    c: Coincident(g6,g-1)
    c: PointOnObject(g5,g-2)
    c: DistanceX(g0,g4) = 5.5
    c: Coincident(g7,g-1)
    c: Radius(g7) = 1.5
FEATURE [PartDesign::Pad] Pad1056  label="M3 Nut Primitive003"
  Length = 1.2
  Length2 = 1.2
  Profile = -> Sketch011
  Type = 4
FEATURE [Sketcher::SketchObject] Sketch012
  ExternalGeometry = -> [Pad1056]
  MapMode = 5
  Placement = pos=(0,0,0) rot=(0.57735,0.57735,0.57735;2.0944rad)
  Support = -> [YZ_Plane006]
  sketch-geometry (6):
    g0: LineSegment StartX=-2.67543 StartY=1.2 StartZ=0 EndX=-3.67543 EndY=1.2 EndZ=0
    g1: LineSegment StartX=-3.67543 StartY=1.2 StartZ=0 EndX=-3.67543 EndY=-1.2 EndZ=0
    g2: LineSegment StartX=-3.67543 StartY=-1.2 StartZ=0 EndX=-2.67543 EndY=-1.2 EndZ=0
    g3: LineSegment StartX=-2.67543 StartY=-1.2 StartZ=0 EndX=-3.17543 EndY=-1 EndZ=0
    g4: LineSegment StartX=-3.17543 StartY=-1 StartZ=0 EndX=-3.17543 EndY=1 EndZ=0
    g5: LineSegment StartX=-3.17543 StartY=1 StartZ=0 EndX=-2.67543 EndY=1.2 EndZ=0
  constraints (15):
    c: Horizontal(g0)
    c: Coincident(g0,g1)
    c: Coincident(g1,g2)
    c: Coincident(g2,g3)
    c: Coincident(g3,g4)
    c: Coincident(g4,g5)
    c: Coincident(g5,g0)
    c: Symmetric(g4,g3,g-1)
    c: Symmetric(g0,g2,g-1)
    c: Symmetric(g1,g0,g-1)
    c: DistanceX(g0,g4) = 0.5
    c: DistanceY(g3,g4) = 2
    c: DistanceY(g1,g0) = 2.4
    c: PointOnObject(g3,g-3)
    c: DistanceX(g4,g0) = 0.5
FEATURE [PartDesign::Groove] Groove003  label="M3 Nut Smooth003"
  Angle = 360
  Axis = (-2e-16,3e-16,1)
  Base = (0,0,0)
  BaseFeature = -> Pad1056
  Profile = -> Sketch012
  ReferenceAxis = -> Sketch012 [V_Axis]
  Reversed = true
FEATURE [PartDesign::Chamfer] Chamfer003  label="M3 Nut Smooth Hole003"
  Base = -> Groove003 [Edge24,Edge23]
  BaseFeature = -> Groove003
  Size = 0.2
FEATURE [PartDesign::Body] Body006  label="M3 Nut116"
  Group = -> [Sketch011,Pad1056,Sketch012,Groove003,Chamfer003]
  Origin = -> Origin006
  Placement = pos=(-7.5,70.5,1.6e-14) rot=(1,0,0;1.5708rad)
  Tip = -> Chamfer003
FEATURE [App::Part] Part264  label="Chassis Right Side Nuts"
  Group = -> [Body672,Body004,Body678,Body006]
  Origin = -> Origin960
  Placement = pos=(3.25,0,-1.8e-15) rot=(0,1,0;1.5708rad)
FEATURE [App::Part] Part012  label="Chassis All"
  Group = -> [Part264,Body007,Body673,Body666,Part001,Part005,Part006,Part010,Part011]
  Origin = -> Origin053
  Placement = pos=(-108,-45,204) rot=(0,0,1;4.71239rad)
FEATURE [Sketcher::SketchObject] Sketch2389
  MapMode = 5
  Support = -> [XY_Plane972]
  sketch-geometry (1):
    g0: Circle CenterX=0 CenterY=0 CenterZ=0 NormalX=0 NormalY=0 NormalZ=1 AngleXU=0 Radius=8
  constraints (2):
    c: Coincident(g0,g-1)
    c: Radius(g0) = 8
FEATURE [Sketcher::SketchObject] Sketch2393
  MapMode = 5
  Support = -> [XY_Plane974]
  sketch-geometry (2):
    g0: Circle CenterX=0 CenterY=0 CenterZ=0 NormalX=0 NormalY=0 NormalZ=1 AngleXU=0 Radius=4
    g1: Circle CenterX=0 CenterY=0 CenterZ=0 NormalX=0 NormalY=0 NormalZ=1 AngleXU=0 Radius=6.25
  constraints (4):
    c: Coincident(g0,g-1)
    c: Coincident(g1,g0)
    c: Radius(g0) = 4
    c: Radius(g1) = 6.25
FEATURE [PartDesign::Body] Body680
  Origin = -> Origin973
FEATURE [PartDesign::Pad] Pad1057
  Length = 5
  Length2 = 100
  Profile = -> Sketch2389
  Type = 0
FEATURE [Sketcher::SketchObject] Sketch2391
  MapMode = 5
  Placement = pos=(0,0,0) rot=(1,0,0;3.14159rad)
  Support = -> [Pad1057]
  sketch-geometry (1):
    g0: Circle CenterX=0 CenterY=0 CenterZ=0 NormalX=0 NormalY=0 NormalZ=1 AngleXU=0 Radius=2.5
  constraints (2):
    c: Coincident(g0,g-1)
    c: Radius(g0) = 2.5
FEATURE [PartDesign::Pocket] Pocket845
  BaseFeature = -> Pad1057
  Length = 5
  Length2 = 100
  Profile = -> Sketch2391
  Type = 0
FEATURE [Sketcher::SketchObject] Sketch2390
  MapMode = 5
  Placement = pos=(0,0,0) rot=(1,0,0;3.14159rad)
  Support = -> [Pocket845]
  sketch-geometry (2):
    g0: Circle CenterX=0 CenterY=0 CenterZ=0 NormalX=0 NormalY=0 NormalZ=1 AngleXU=0 Radius=3.5
    g1: Circle CenterX=0 CenterY=0 CenterZ=0 NormalX=0 NormalY=0 NormalZ=1 AngleXU=0 Radius=7
  constraints (4):
    c: Coincident(g0,g-1)
    c: Coincident(g1,g0)
    c: Radius(g0) = 3.5
    c: Radius(g1) = 7
FEATURE [PartDesign::Pocket] Pocket847
  BaseFeature = -> Pocket845
  Length = 0.5
  Length2 = 100
  Profile = -> Sketch2390
  Type = 0
FEATURE [Sketcher::SketchObject] Sketch2392
  MapMode = 5
  Placement = pos=(0,0,5) rot=(0,0,1;0rad)
  Support = -> [Pocket847]
  sketch-geometry (2):
    g0: Circle CenterX=0 CenterY=0 CenterZ=0 NormalX=0 NormalY=0 NormalZ=1 AngleXU=0 Radius=3.5
    g1: Circle CenterX=0 CenterY=0 CenterZ=0 NormalX=0 NormalY=0 NormalZ=1 AngleXU=0 Radius=7
  constraints (4):
    c: Coincident(g0,g-1)
    c: Coincident(g1,g0)
    c: Radius(g0) = 3.5
    c: Radius(g1) = 7
FEATURE [PartDesign::Pocket] Pocket846
  BaseFeature = -> Pocket847
  Length = 0.5
  Length2 = 100
  Profile = -> Sketch2392
  Type = 0
FEATURE [PartDesign::Chamfer] Chamfer523
  Base = -> Pocket846 [Face10,Face2,Face3,Face11]
  BaseFeature = -> Pocket846
  Size = 0.25
FEATURE [PartDesign::Body] Body679
  Group = -> [Sketch2389,Pad1057,Sketch2391,Pocket845,Sketch2390,Pocket847,Sketch2392,Pocket846,Chamfer523]
  Origin = -> Origin974
  Tip = -> Chamfer523
FEATURE [PartDesign::Pad] Pad1058
  Length = 5
  Length2 = 100
  Profile = -> Sketch2393
  Type = 0
FEATURE [PartDesign::Chamfer] Chamfer522
  Base = -> Pad1058 [Face3,Face4]
  BaseFeature = -> Pad1058
  Size = 0.2
FEATURE [PartDesign::Body] Body681
  Group = -> [Sketch2393,Pad1058,Chamfer522]
  Origin = -> Origin975
  Tip = -> Chamfer522
FEATURE [App::Part] Part270  label="Ball Bearing006"
  Group = -> [Body679,Body681,Body680]
  Origin = -> Origin976
  Placement = pos=(-189,-139.25,211.25) rot=(0,1,0;1.5708rad)
FEATURE [Sketcher::SketchObject] Sketch2394
  MapMode = 5
  Support = -> [XY_Plane976]
  sketch-geometry (1):
    g0: Circle CenterX=0 CenterY=0 CenterZ=0 NormalX=0 NormalY=0 NormalZ=1 AngleXU=0 Radius=8
  constraints (2):
    c: Coincident(g0,g-1)
    c: Radius(g0) = 8
FEATURE [Sketcher::SketchObject] Sketch2398
  MapMode = 5
  Support = -> [XY_Plane978]
  sketch-geometry (2):
    g0: Circle CenterX=0 CenterY=0 CenterZ=0 NormalX=0 NormalY=0 NormalZ=1 AngleXU=0 Radius=4
    g1: Circle CenterX=0 CenterY=0 CenterZ=0 NormalX=0 NormalY=0 NormalZ=1 AngleXU=0 Radius=6.25
  constraints (4):
    c: Coincident(g0,g-1)
    c: Coincident(g1,g0)
    c: Radius(g0) = 4
    c: Radius(g1) = 6.25
FEATURE [PartDesign::Body] Body683
  Origin = -> Origin977
FEATURE [PartDesign::Pad] Pad1059
  Length = 5
  Length2 = 100
  Profile = -> Sketch2394
  Type = 0
FEATURE [Sketcher::SketchObject] Sketch2396
  MapMode = 5
  Placement = pos=(0,0,0) rot=(1,0,0;3.14159rad)
  Support = -> [Pad1059]
  sketch-geometry (1):
    g0: Circle CenterX=0 CenterY=0 CenterZ=0 NormalX=0 NormalY=0 NormalZ=1 AngleXU=0 Radius=2.5
  constraints (2):
    c: Coincident(g0,g-1)
    c: Radius(g0) = 2.5
FEATURE [PartDesign::Pocket] Pocket848
  BaseFeature = -> Pad1059
  Length = 5
  Length2 = 100
  Profile = -> Sketch2396
  Type = 0
FEATURE [Sketcher::SketchObject] Sketch2395
  MapMode = 5
  Placement = pos=(0,0,0) rot=(1,0,0;3.14159rad)
  Support = -> [Pocket848]
  sketch-geometry (2):
    g0: Circle CenterX=0 CenterY=0 CenterZ=0 NormalX=0 NormalY=0 NormalZ=1 AngleXU=0 Radius=3.5
    g1: Circle CenterX=0 CenterY=0 CenterZ=0 NormalX=0 NormalY=0 NormalZ=1 AngleXU=0 Radius=7
  constraints (4):
    c: Coincident(g0,g-1)
    c: Coincident(g1,g0)
    c: Radius(g0) = 3.5
    c: Radius(g1) = 7
FEATURE [PartDesign::Pocket] Pocket850
  BaseFeature = -> Pocket848
  Length = 0.5
  Length2 = 100
  Profile = -> Sketch2395
  Type = 0
FEATURE [Sketcher::SketchObject] Sketch2397
  MapMode = 5
  Placement = pos=(0,0,5) rot=(0,0,1;0rad)
  Support = -> [Pocket850]
  sketch-geometry (2):
    g0: Circle CenterX=0 CenterY=0 CenterZ=0 NormalX=0 NormalY=0 NormalZ=1 AngleXU=0 Radius=3.5
    g1: Circle CenterX=0 CenterY=0 CenterZ=0 NormalX=0 NormalY=0 NormalZ=1 AngleXU=0 Radius=7
  constraints (4):
    c: Coincident(g0,g-1)
    c: Coincident(g1,g0)
    c: Radius(g0) = 3.5
    c: Radius(g1) = 7
FEATURE [PartDesign::Pocket] Pocket849
  BaseFeature = -> Pocket850
  Length = 0.5
  Length2 = 100
  Profile = -> Sketch2397
  Type = 0
FEATURE [PartDesign::Chamfer] Chamfer525
  Base = -> Pocket849 [Face10,Face2,Face3,Face11]
  BaseFeature = -> Pocket849
  Size = 0.25
FEATURE [PartDesign::Body] Body682
  Group = -> [Sketch2394,Pad1059,Sketch2396,Pocket848,Sketch2395,Pocket850,Sketch2397,Pocket849,Chamfer525]
  Origin = -> Origin978
  Tip = -> Chamfer525
FEATURE [PartDesign::Pad] Pad1060
  Length = 5
  Length2 = 100
  Profile = -> Sketch2398
  Type = 0
FEATURE [PartDesign::Chamfer] Chamfer524
  Base = -> Pad1060 [Face3,Face4]
  BaseFeature = -> Pad1060
  Size = 0.2
FEATURE [PartDesign::Body] Body684
  Group = -> [Sketch2398,Pad1060,Chamfer524]
  Origin = -> Origin979
  Tip = -> Chamfer524
FEATURE [App::Part] Part271  label="Ball Bearing007"
  Group = -> [Body682,Body684,Body683]
  Origin = -> Origin980
  Placement = pos=(-189,-60.25,210.5) rot=(0,1,0;1.5708rad)
FEATURE [Sketcher::SketchObject] Sketch2399
  MapMode = 5
  Support = -> [XY_Plane980]
  sketch-geometry (1):
    g0: Circle CenterX=0 CenterY=0 CenterZ=0 NormalX=0 NormalY=0 NormalZ=1 AngleXU=0 Radius=8
  constraints (2):
    c: Coincident(g0,g-1)
    c: Radius(g0) = 8
FEATURE [Sketcher::SketchObject] Sketch2403
  MapMode = 5
  Support = -> [XY_Plane982]
  sketch-geometry (2):
    g0: Circle CenterX=0 CenterY=0 CenterZ=0 NormalX=0 NormalY=0 NormalZ=1 AngleXU=0 Radius=4
    g1: Circle CenterX=0 CenterY=0 CenterZ=0 NormalX=0 NormalY=0 NormalZ=1 AngleXU=0 Radius=6.25
  constraints (4):
    c: Coincident(g0,g-1)
    c: Coincident(g1,g0)
    c: Radius(g0) = 4
    c: Radius(g1) = 6.25
FEATURE [PartDesign::Body] Body686
  Origin = -> Origin981
FEATURE [PartDesign::Pad] Pad1061
  Length = 5
  Length2 = 100
  Profile = -> Sketch2399
  Type = 0
FEATURE [Sketcher::SketchObject] Sketch2401
  MapMode = 5
  Placement = pos=(0,0,0) rot=(1,0,0;3.14159rad)
  Support = -> [Pad1061]
  sketch-geometry (1):
    g0: Circle CenterX=0 CenterY=0 CenterZ=0 NormalX=0 NormalY=0 NormalZ=1 AngleXU=0 Radius=2.5
  constraints (2):
    c: Coincident(g0,g-1)
    c: Radius(g0) = 2.5
FEATURE [PartDesign::Pocket] Pocket851
  BaseFeature = -> Pad1061
  Length = 5
  Length2 = 100
  Profile = -> Sketch2401
  Type = 0
FEATURE [Sketcher::SketchObject] Sketch2400
  MapMode = 5
  Placement = pos=(0,0,0) rot=(1,0,0;3.14159rad)
  Support = -> [Pocket851]
  sketch-geometry (2):
    g0: Circle CenterX=0 CenterY=0 CenterZ=0 NormalX=0 NormalY=0 NormalZ=1 AngleXU=0 Radius=3.5
    g1: Circle CenterX=0 CenterY=0 CenterZ=0 NormalX=0 NormalY=0 NormalZ=1 AngleXU=0 Radius=7
  constraints (4):
    c: Coincident(g0,g-1)
    c: Coincident(g1,g0)
    c: Radius(g0) = 3.5
    c: Radius(g1) = 7
FEATURE [PartDesign::Pocket] Pocket853
  BaseFeature = -> Pocket851
  Length = 0.5
  Length2 = 100
  Profile = -> Sketch2400
  Type = 0
FEATURE [Sketcher::SketchObject] Sketch2402
  MapMode = 5
  Placement = pos=(0,0,5) rot=(0,0,1;0rad)
  Support = -> [Pocket853]
  sketch-geometry (2):
    g0: Circle CenterX=0 CenterY=0 CenterZ=0 NormalX=0 NormalY=0 NormalZ=1 AngleXU=0 Radius=3.5
    g1: Circle CenterX=0 CenterY=0 CenterZ=0 NormalX=0 NormalY=0 NormalZ=1 AngleXU=0 Radius=7
  constraints (4):
    c: Coincident(g0,g-1)
    c: Coincident(g1,g0)
    c: Radius(g0) = 3.5
    c: Radius(g1) = 7
FEATURE [PartDesign::Pocket] Pocket852
  BaseFeature = -> Pocket853
  Length = 0.5
  Length2 = 100
  Profile = -> Sketch2402
  Type = 0
FEATURE [PartDesign::Chamfer] Chamfer527
  Base = -> Pocket852 [Face10,Face2,Face3,Face11]
  BaseFeature = -> Pocket852
  Size = 0.25
FEATURE [PartDesign::Body] Body685
  Group = -> [Sketch2399,Pad1061,Sketch2401,Pocket851,Sketch2400,Pocket853,Sketch2402,Pocket852,Chamfer527]
  Origin = -> Origin982
  Tip = -> Chamfer527
FEATURE [PartDesign::Pad] Pad1062
  Length = 5
  Length2 = 100
  Profile = -> Sketch2403
  Type = 0
FEATURE [PartDesign::Chamfer] Chamfer526
  Base = -> Pad1062 [Face3,Face4]
  BaseFeature = -> Pad1062
  Size = 0.2
FEATURE [PartDesign::Body] Body687
  Group = -> [Sketch2403,Pad1062,Chamfer526]
  Origin = -> Origin983
  Tip = -> Chamfer526
FEATURE [App::Part] Part272  label="Ball Bearing008"
  Group = -> [Body685,Body687,Body686]
  Origin = -> Origin984
  Placement = pos=(-32.25,-60.75,211.25) rot=(0,1,0;1.5708rad)
FEATURE [Sketcher::SketchObject] Sketch2404
  MapMode = 5
  Support = -> [XY_Plane984]
  sketch-geometry (1):
    g0: Circle CenterX=0 CenterY=0 CenterZ=0 NormalX=0 NormalY=0 NormalZ=1 AngleXU=0 Radius=8
  constraints (2):
    c: Coincident(g0,g-1)
    c: Radius(g0) = 8
FEATURE [Sketcher::SketchObject] Sketch2408
  MapMode = 5
  Support = -> [XY_Plane986]
  sketch-geometry (2):
    g0: Circle CenterX=0 CenterY=0 CenterZ=0 NormalX=0 NormalY=0 NormalZ=1 AngleXU=0 Radius=4
    g1: Circle CenterX=0 CenterY=0 CenterZ=0 NormalX=0 NormalY=0 NormalZ=1 AngleXU=0 Radius=6.25
  constraints (4):
    c: Coincident(g0,g-1)
    c: Coincident(g1,g0)
    c: Radius(g0) = 4
    c: Radius(g1) = 6.25
FEATURE [PartDesign::Body] Body689
  Origin = -> Origin985
FEATURE [PartDesign::Pad] Pad1063
  Length = 5
  Length2 = 100
  Profile = -> Sketch2404
  Type = 0
FEATURE [Sketcher::SketchObject] Sketch2406
  MapMode = 5
  Placement = pos=(0,0,0) rot=(1,0,0;3.14159rad)
  Support = -> [Pad1063]
  sketch-geometry (1):
    g0: Circle CenterX=0 CenterY=0 CenterZ=0 NormalX=0 NormalY=0 NormalZ=1 AngleXU=0 Radius=2.5
  constraints (2):
    c: Coincident(g0,g-1)
    c: Radius(g0) = 2.5
FEATURE [PartDesign::Pocket] Pocket854
  BaseFeature = -> Pad1063
  Length = 5
  Length2 = 100
  Profile = -> Sketch2406
  Type = 0
FEATURE [Sketcher::SketchObject] Sketch2405
  MapMode = 5
  Placement = pos=(0,0,0) rot=(1,0,0;3.14159rad)
  Support = -> [Pocket854]
  sketch-geometry (2):
    g0: Circle CenterX=0 CenterY=0 CenterZ=0 NormalX=0 NormalY=0 NormalZ=1 AngleXU=0 Radius=3.5
    g1: Circle CenterX=0 CenterY=0 CenterZ=0 NormalX=0 NormalY=0 NormalZ=1 AngleXU=0 Radius=7
  constraints (4):
    c: Coincident(g0,g-1)
    c: Coincident(g1,g0)
    c: Radius(g0) = 3.5
    c: Radius(g1) = 7
FEATURE [PartDesign::Pocket] Pocket856
  BaseFeature = -> Pocket854
  Length = 0.5
  Length2 = 100
  Profile = -> Sketch2405
  Type = 0
FEATURE [Sketcher::SketchObject] Sketch2407
  MapMode = 5
  Placement = pos=(0,0,5) rot=(0,0,1;0rad)
  Support = -> [Pocket856]
  sketch-geometry (2):
    g0: Circle CenterX=0 CenterY=0 CenterZ=0 NormalX=0 NormalY=0 NormalZ=1 AngleXU=0 Radius=3.5
    g1: Circle CenterX=0 CenterY=0 CenterZ=0 NormalX=0 NormalY=0 NormalZ=1 AngleXU=0 Radius=7
  constraints (4):
    c: Coincident(g0,g-1)
    c: Coincident(g1,g0)
    c: Radius(g0) = 3.5
    c: Radius(g1) = 7
FEATURE [PartDesign::Pocket] Pocket855
  BaseFeature = -> Pocket856
  Length = 0.5
  Length2 = 100
  Profile = -> Sketch2407
  Type = 0
FEATURE [PartDesign::Chamfer] Chamfer529
  Base = -> Pocket855 [Face10,Face2,Face3,Face11]
  BaseFeature = -> Pocket855
  Size = 0.25
FEATURE [PartDesign::Body] Body688
  Group = -> [Sketch2404,Pad1063,Sketch2406,Pocket854,Sketch2405,Pocket856,Sketch2407,Pocket855,Chamfer529]
  Origin = -> Origin986
  Tip = -> Chamfer529
FEATURE [PartDesign::Pad] Pad1064
  Length = 5
  Length2 = 100
  Profile = -> Sketch2408
  Type = 0
FEATURE [PartDesign::Chamfer] Chamfer528
  Base = -> Pad1064 [Face3,Face4]
  BaseFeature = -> Pad1064
  Size = 0.2
FEATURE [PartDesign::Body] Body690
  Group = -> [Sketch2408,Pad1064,Chamfer528]
  Origin = -> Origin987
  Tip = -> Chamfer528
FEATURE [App::Part] Part273  label="Ball Bearing009"
  Group = -> [Body688,Body690,Body689]
  Origin = -> Origin988
  Placement = pos=(-32,-138.75,210.5) rot=(0,1,0;1.5708rad)
FEATURE [Sketcher::SketchObject] Sketch2409  label="Inverse Kinematics Body"
  Placement = pos=(0,0,300) rot=(0,0,1;0rad)
  sketch-geometry (4):
    g0: LineSegment [constr] StartX=-211.207 StartY=-138.966 StartZ=0 EndX=-3.70748 EndY=-138.966 EndZ=0
    g1: LineSegment [constr] StartX=-3.70748 StartY=-138.966 StartZ=0 EndX=-3.70748 EndY=-60.9658 EndZ=0
    g2: LineSegment [constr] StartX=-3.70748 StartY=-60.9658 StartZ=0 EndX=-211.207 EndY=-60.9658 EndZ=0
    g3: LineSegment [constr] StartX=-211.207 StartY=-60.9658 StartZ=0 EndX=-211.207 EndY=-138.966 EndZ=0
  constraints (10):
    c: Coincident(g0,g1)
    c: Coincident(g1,g2)
    c: Coincident(g2,g3)
    c: Coincident(g3,g0)
    c: Horizontal(g0)
    c: Horizontal(g2)
    c: Vertical(g1)
    c: Vertical(g3)
    c: DistanceX(g2,g2) = 207.5
    c: DistanceY(g3,g3) = 78
FEATURE [Sketcher::SketchObject] Sketch2410
  MapMode = 5
  Support = -> [XY_Plane987]
  sketch-geometry (8):
    g0: LineSegment StartX=0 StartY=3.17543 StartZ=0 EndX=-2.75 EndY=1.58771 EndZ=0
    g1: LineSegment StartX=-2.75 StartY=1.58771 StartZ=0 EndX=-2.75 EndY=-1.58771 EndZ=0
    g2: LineSegment StartX=-2.75 StartY=-1.58771 StartZ=0 EndX=0 EndY=-3.17543 EndZ=0
    g3: LineSegment StartX=0 StartY=-3.17543 StartZ=0 EndX=2.75 EndY=-1.58771 EndZ=0
    g4: LineSegment StartX=2.75 StartY=-1.58771 StartZ=0 EndX=2.75 EndY=1.58771 EndZ=0
    g5: LineSegment StartX=2.75 StartY=1.58771 StartZ=0 EndX=0 EndY=3.17543 EndZ=0
    g6: Circle [constr] CenterX=0 CenterY=0 CenterZ=0 NormalX=0 NormalY=0 NormalZ=1 AngleXU=0 Radius=3.17543
    g7: Circle CenterX=0 CenterY=0 CenterZ=0 NormalX=0 NormalY=0 NormalZ=1 AngleXU=0 Radius=1.5
  constraints (18):
    c: Coincident(g0,g1)
    c: Coincident(g1,g2)
    c: Coincident(g2,g3)
    c: Coincident(g3,g4)
    c: Coincident(g4,g5)
    c: Coincident(g5,g0)
    c: Equal(g0, g1-g5) x5
    c: PointOnObject(g0,g6)
    c: PointOnObject(g1,g6)
    c: PointOnObject(g2,g6)
    c: PointOnObject(g3,g6)
    c: PointOnObject(g4,g6)
    c: PointOnObject(g5,g6)
    c: Coincident(g6,g-1)
    c: PointOnObject(g5,g-2)
    c: DistanceX(g0,g4) = 5.5
    c: Coincident(g7,g-1)
    c: Radius(g7) = 1.5
FEATURE [PartDesign::Pad] Pad1065  label="M3 Nut Primitive213"
  Length = 1.2
  Length2 = 1.2
  Profile = -> Sketch2410
  Type = 4
FEATURE [Sketcher::SketchObject] Sketch2411
  ExternalGeometry = -> [Pad1065]
  MapMode = 5
  Placement = pos=(0,0,0) rot=(0.57735,0.57735,0.57735;2.0944rad)
  Support = -> [YZ_Plane981]
  sketch-geometry (6):
    g0: LineSegment StartX=-2.67543 StartY=1.2 StartZ=0 EndX=-3.67543 EndY=1.2 EndZ=0
    g1: LineSegment StartX=-3.67543 StartY=1.2 StartZ=0 EndX=-3.67543 EndY=-1.2 EndZ=0
    g2: LineSegment StartX=-3.67543 StartY=-1.2 StartZ=0 EndX=-2.67543 EndY=-1.2 EndZ=0
    g3: LineSegment StartX=-2.67543 StartY=-1.2 StartZ=0 EndX=-3.17543 EndY=-1 EndZ=0
    g4: LineSegment StartX=-3.17543 StartY=-1 StartZ=0 EndX=-3.17543 EndY=1 EndZ=0
    g5: LineSegment StartX=-3.17543 StartY=1 StartZ=0 EndX=-2.67543 EndY=1.2 EndZ=0
  constraints (15):
    c: Horizontal(g0)
    c: Coincident(g0,g1)
    c: Coincident(g1,g2)
    c: Coincident(g2,g3)
    c: Coincident(g3,g4)
    c: Coincident(g4,g5)
    c: Coincident(g5,g0)
    c: Symmetric(g4,g3,g-1)
    c: Symmetric(g0,g2,g-1)
    c: Symmetric(g1,g0,g-1)
    c: DistanceX(g0,g4) = 0.5
    c: DistanceY(g3,g4) = 2
    c: DistanceY(g1,g0) = 2.4
    c: PointOnObject(g3,g-3)
    c: DistanceX(g4,g0) = 0.5
FEATURE [PartDesign::Groove] Groove221  label="M3 Nut Smooth213"
  Angle = 360
  Axis = (-2e-16,3e-16,1)
  Base = (0,0,0)
  BaseFeature = -> Pad1065
  Profile = -> Sketch2411
  ReferenceAxis = -> Sketch2411 [V_Axis]
  Reversed = true
FEATURE [PartDesign::Chamfer] Chamfer530  label="M3 Nut Smooth Hole213"
  Base = -> Groove221 [Edge24,Edge23]
  BaseFeature = -> Groove221
  Size = 0.2
FEATURE [PartDesign::Body] Body691  label="M3 Nut117"
  Group = -> [Sketch2410,Pad1065,Sketch2411,Groove221,Chamfer530]
  Origin = -> Origin989
  Placement = pos=(0,-1.63e-14,73.25) rot=(-0.57735,0.57735,0.57735;4.18879rad)
  Tip = -> Chamfer530
FEATURE [Sketcher::SketchObject] Sketch2412
  MapMode = 5
  Support = -> [XY_Plane988]
  sketch-geometry (8):
    g0: LineSegment StartX=0 StartY=3.17543 StartZ=0 EndX=-2.75 EndY=1.58771 EndZ=0
    g1: LineSegment StartX=-2.75 StartY=1.58771 StartZ=0 EndX=-2.75 EndY=-1.58771 EndZ=0
    g2: LineSegment StartX=-2.75 StartY=-1.58771 StartZ=0 EndX=0 EndY=-3.17543 EndZ=0
    g3: LineSegment StartX=0 StartY=-3.17543 StartZ=0 EndX=2.75 EndY=-1.58771 EndZ=0
    g4: LineSegment StartX=2.75 StartY=-1.58771 StartZ=0 EndX=2.75 EndY=1.58771 EndZ=0
    g5: LineSegment StartX=2.75 StartY=1.58771 StartZ=0 EndX=0 EndY=3.17543 EndZ=0
    g6: Circle [constr] CenterX=0 CenterY=0 CenterZ=0 NormalX=0 NormalY=0 NormalZ=1 AngleXU=0 Radius=3.17543
    g7: Circle CenterX=0 CenterY=0 CenterZ=0 NormalX=0 NormalY=0 NormalZ=1 AngleXU=0 Radius=1.5
  constraints (18):
    c: Coincident(g0,g1)
    c: Coincident(g1,g2)
    c: Coincident(g2,g3)
    c: Coincident(g3,g4)
    c: Coincident(g4,g5)
    c: Coincident(g5,g0)
    c: Equal(g0, g1-g5) x5
    c: PointOnObject(g0,g6)
    c: PointOnObject(g1,g6)
    c: PointOnObject(g2,g6)
    c: PointOnObject(g3,g6)
    c: PointOnObject(g4,g6)
    c: PointOnObject(g5,g6)
    c: Coincident(g6,g-1)
    c: PointOnObject(g5,g-2)
    c: DistanceX(g0,g4) = 5.5
    c: Coincident(g7,g-1)
    c: Radius(g7) = 1.5
FEATURE [PartDesign::Pad] Pad1066  label="M3 Nut Primitive214"
  Length = 1.2
  Length2 = 1.2
  Profile = -> Sketch2412
  Type = 4
FEATURE [Sketcher::SketchObject] Sketch2413
  ExternalGeometry = -> [Pad1066]
  MapMode = 5
  Placement = pos=(0,0,0) rot=(0.57735,0.57735,0.57735;2.0944rad)
  Support = -> [YZ_Plane982]
  sketch-geometry (6):
    g0: LineSegment StartX=-2.67543 StartY=1.2 StartZ=0 EndX=-3.67543 EndY=1.2 EndZ=0
    g1: LineSegment StartX=-3.67543 StartY=1.2 StartZ=0 EndX=-3.67543 EndY=-1.2 EndZ=0
    g2: LineSegment StartX=-3.67543 StartY=-1.2 StartZ=0 EndX=-2.67543 EndY=-1.2 EndZ=0
    g3: LineSegment StartX=-2.67543 StartY=-1.2 StartZ=0 EndX=-3.17543 EndY=-1 EndZ=0
    g4: LineSegment StartX=-3.17543 StartY=-1 StartZ=0 EndX=-3.17543 EndY=1 EndZ=0
    g5: LineSegment StartX=-3.17543 StartY=1 StartZ=0 EndX=-2.67543 EndY=1.2 EndZ=0
  constraints (15):
    c: Horizontal(g0)
    c: Coincident(g0,g1)
    c: Coincident(g1,g2)
    c: Coincident(g2,g3)
    c: Coincident(g3,g4)
    c: Coincident(g4,g5)
    c: Coincident(g5,g0)
    c: Symmetric(g4,g3,g-1)
    c: Symmetric(g0,g2,g-1)
    c: Symmetric(g1,g0,g-1)
    c: DistanceX(g0,g4) = 0.5
    c: DistanceY(g3,g4) = 2
    c: DistanceY(g1,g0) = 2.4
    c: PointOnObject(g3,g-3)
    c: DistanceX(g4,g0) = 0.5
FEATURE [PartDesign::Groove] Groove222  label="M3 Nut Smooth214"
  Angle = 360
  Axis = (-2e-16,3e-16,1)
  Base = (0,0,0)
  BaseFeature = -> Pad1066
  Profile = -> Sketch2413
  ReferenceAxis = -> Sketch2413 [V_Axis]
  Reversed = true
FEATURE [PartDesign::Chamfer] Chamfer531  label="M3 Nut Smooth Hole214"
  Base = -> Groove222 [Edge24,Edge23]
  BaseFeature = -> Groove222
  Size = 0.2
FEATURE [PartDesign::Body] Body692  label="M3 Nut118"
  Group = -> [Sketch2412,Pad1066,Sketch2413,Groove222,Chamfer531]
  Origin = -> Origin990
  Placement = pos=(1.33e-14,30,73.25) rot=(-0.57735,0.57735,0.57735;4.18879rad)
  Tip = -> Chamfer531
FEATURE [Sketcher::SketchObject] Sketch2414
  MapMode = 5
  Support = -> [XY_Plane989]
  sketch-geometry (8):
    g0: LineSegment StartX=0 StartY=3.17543 StartZ=0 EndX=-2.75 EndY=1.58771 EndZ=0
    g1: LineSegment StartX=-2.75 StartY=1.58771 StartZ=0 EndX=-2.75 EndY=-1.58771 EndZ=0
    g2: LineSegment StartX=-2.75 StartY=-1.58771 StartZ=0 EndX=0 EndY=-3.17543 EndZ=0
    g3: LineSegment StartX=0 StartY=-3.17543 StartZ=0 EndX=2.75 EndY=-1.58771 EndZ=0
    g4: LineSegment StartX=2.75 StartY=-1.58771 StartZ=0 EndX=2.75 EndY=1.58771 EndZ=0
    g5: LineSegment StartX=2.75 StartY=1.58771 StartZ=0 EndX=0 EndY=3.17543 EndZ=0
    g6: Circle [constr] CenterX=0 CenterY=0 CenterZ=0 NormalX=0 NormalY=0 NormalZ=1 AngleXU=0 Radius=3.17543
    g7: Circle CenterX=0 CenterY=0 CenterZ=0 NormalX=0 NormalY=0 NormalZ=1 AngleXU=0 Radius=1.5
  constraints (18):
    c: Coincident(g0,g1)
    c: Coincident(g1,g2)
    c: Coincident(g2,g3)
    c: Coincident(g3,g4)
    c: Coincident(g4,g5)
    c: Coincident(g5,g0)
    c: Equal(g0, g1-g5) x5
    c: PointOnObject(g0,g6)
    c: PointOnObject(g1,g6)
    c: PointOnObject(g2,g6)
    c: PointOnObject(g3,g6)
    c: PointOnObject(g4,g6)
    c: PointOnObject(g5,g6)
    c: Coincident(g6,g-1)
    c: PointOnObject(g5,g-2)
    c: DistanceX(g0,g4) = 5.5
    c: Coincident(g7,g-1)
    c: Radius(g7) = 1.5
FEATURE [PartDesign::Pad] Pad1067  label="M3 Nut Primitive215"
  Length = 1.2
  Length2 = 1.2
  Profile = -> Sketch2414
  Type = 4
FEATURE [Sketcher::SketchObject] Sketch2415
  ExternalGeometry = -> [Pad1067]
  MapMode = 5
  Placement = pos=(0,0,0) rot=(0.57735,0.57735,0.57735;2.0944rad)
  Support = -> [YZ_Plane983]
  sketch-geometry (6):
    g0: LineSegment StartX=-2.67543 StartY=1.2 StartZ=0 EndX=-3.67543 EndY=1.2 EndZ=0
    g1: LineSegment StartX=-3.67543 StartY=1.2 StartZ=0 EndX=-3.67543 EndY=-1.2 EndZ=0
    g2: LineSegment StartX=-3.67543 StartY=-1.2 StartZ=0 EndX=-2.67543 EndY=-1.2 EndZ=0
    g3: LineSegment StartX=-2.67543 StartY=-1.2 StartZ=0 EndX=-3.17543 EndY=-1 EndZ=0
    g4: LineSegment StartX=-3.17543 StartY=-1 StartZ=0 EndX=-3.17543 EndY=1 EndZ=0
    g5: LineSegment StartX=-3.17543 StartY=1 StartZ=0 EndX=-2.67543 EndY=1.2 EndZ=0
  constraints (15):
    c: Horizontal(g0)
    c: Coincident(g0,g1)
    c: Coincident(g1,g2)
    c: Coincident(g2,g3)
    c: Coincident(g3,g4)
    c: Coincident(g4,g5)
    c: Coincident(g5,g0)
    c: Symmetric(g4,g3,g-1)
    c: Symmetric(g0,g2,g-1)
    c: Symmetric(g1,g0,g-1)
    c: DistanceX(g0,g4) = 0.5
    c: DistanceY(g3,g4) = 2
    c: DistanceY(g1,g0) = 2.4
    c: PointOnObject(g3,g-3)
    c: DistanceX(g4,g0) = 0.5
FEATURE [PartDesign::Groove] Groove223  label="M3 Nut Smooth215"
  Angle = 360
  Axis = (-2e-16,3e-16,1)
  Base = (0,0,0)
  BaseFeature = -> Pad1067
  Profile = -> Sketch2415
  ReferenceAxis = -> Sketch2415 [V_Axis]
  Reversed = true
FEATURE [PartDesign::Chamfer] Chamfer532  label="M3 Nut Smooth Hole215"
  Base = -> Groove223 [Edge24,Edge23]
  BaseFeature = -> Groove223
  Size = 0.2
FEATURE [PartDesign::Body] Body693  label="M3 Nut119"
  Group = -> [Sketch2414,Pad1067,Sketch2415,Groove223,Chamfer532]
  Origin = -> Origin991
  Placement = pos=(4.4e-15,10,15) rot=(-0.57735,0.57735,0.57735;4.18879rad)
  Tip = -> Chamfer532
FEATURE [Sketcher::SketchObject] Sketch2416
  MapMode = 5
  Support = -> [XY_Plane990]
  sketch-geometry (8):
    g0: LineSegment StartX=0 StartY=3.17543 StartZ=0 EndX=-2.75 EndY=1.58771 EndZ=0
    g1: LineSegment StartX=-2.75 StartY=1.58771 StartZ=0 EndX=-2.75 EndY=-1.58771 EndZ=0
    g2: LineSegment StartX=-2.75 StartY=-1.58771 StartZ=0 EndX=0 EndY=-3.17543 EndZ=0
    g3: LineSegment StartX=0 StartY=-3.17543 StartZ=0 EndX=2.75 EndY=-1.58771 EndZ=0
    g4: LineSegment StartX=2.75 StartY=-1.58771 StartZ=0 EndX=2.75 EndY=1.58771 EndZ=0
    g5: LineSegment StartX=2.75 StartY=1.58771 StartZ=0 EndX=0 EndY=3.17543 EndZ=0
    g6: Circle [constr] CenterX=0 CenterY=0 CenterZ=0 NormalX=0 NormalY=0 NormalZ=1 AngleXU=0 Radius=3.17543
    g7: Circle CenterX=0 CenterY=0 CenterZ=0 NormalX=0 NormalY=0 NormalZ=1 AngleXU=0 Radius=1.5
  constraints (18):
    c: Coincident(g0,g1)
    c: Coincident(g1,g2)
    c: Coincident(g2,g3)
    c: Coincident(g3,g4)
    c: Coincident(g4,g5)
    c: Coincident(g5,g0)
    c: Equal(g0, g1-g5) x5
    c: PointOnObject(g0,g6)
    c: PointOnObject(g1,g6)
    c: PointOnObject(g2,g6)
    c: PointOnObject(g3,g6)
    c: PointOnObject(g4,g6)
    c: PointOnObject(g5,g6)
    c: Coincident(g6,g-1)
    c: PointOnObject(g5,g-2)
    c: DistanceX(g0,g4) = 5.5
    c: Coincident(g7,g-1)
    c: Radius(g7) = 1.5
FEATURE [PartDesign::Pad] Pad1068  label="M3 Nut Primitive216"
  Length = 1.2
  Length2 = 1.2
  Profile = -> Sketch2416
  Type = 4
FEATURE [Sketcher::SketchObject] Sketch2417
  ExternalGeometry = -> [Pad1068]
  MapMode = 5
  Placement = pos=(0,0,0) rot=(0.57735,0.57735,0.57735;2.0944rad)
  Support = -> [YZ_Plane984]
  sketch-geometry (6):
    g0: LineSegment StartX=-2.67543 StartY=1.2 StartZ=0 EndX=-3.67543 EndY=1.2 EndZ=0
    g1: LineSegment StartX=-3.67543 StartY=1.2 StartZ=0 EndX=-3.67543 EndY=-1.2 EndZ=0
    g2: LineSegment StartX=-3.67543 StartY=-1.2 StartZ=0 EndX=-2.67543 EndY=-1.2 EndZ=0
    g3: LineSegment StartX=-2.67543 StartY=-1.2 StartZ=0 EndX=-3.17543 EndY=-1 EndZ=0
    g4: LineSegment StartX=-3.17543 StartY=-1 StartZ=0 EndX=-3.17543 EndY=1 EndZ=0
    g5: LineSegment StartX=-3.17543 StartY=1 StartZ=0 EndX=-2.67543 EndY=1.2 EndZ=0
  constraints (15):
    c: Horizontal(g0)
    c: Coincident(g0,g1)
    c: Coincident(g1,g2)
    c: Coincident(g2,g3)
    c: Coincident(g3,g4)
    c: Coincident(g4,g5)
    c: Coincident(g5,g0)
    c: Symmetric(g4,g3,g-1)
    c: Symmetric(g0,g2,g-1)
    c: Symmetric(g1,g0,g-1)
    c: DistanceX(g0,g4) = 0.5
    c: DistanceY(g3,g4) = 2
    c: DistanceY(g1,g0) = 2.4
    c: PointOnObject(g3,g-3)
    c: DistanceX(g4,g0) = 0.5
FEATURE [PartDesign::Groove] Groove224  label="M3 Nut Smooth216"
  Angle = 360
  Axis = (-2e-16,3e-16,1)
  Base = (0,0,0)
  BaseFeature = -> Pad1068
  Profile = -> Sketch2417
  ReferenceAxis = -> Sketch2417 [V_Axis]
  Reversed = true
FEATURE [PartDesign::Chamfer] Chamfer533  label="M3 Nut Smooth Hole216"
  Base = -> Groove224 [Edge24,Edge23]
  BaseFeature = -> Groove224
  Size = 0.2
FEATURE [PartDesign::Body] Body694  label="M3 Nut120"
  Group = -> [Sketch2416,Pad1068,Sketch2417,Groove224,Chamfer533]
  Origin = -> Origin992
  Placement = pos=(8.9e-15,20,15) rot=(-0.57735,0.57735,0.57735;4.18879rad)
  Tip = -> Chamfer533
FEATURE [App::Part] Part274  label="Front Shoulder Nuts"
  Group = -> [Body691,Body692,Body693,Body694]
  Origin = -> Origin993
  Placement = pos=(15,-115,157.5) rot=(0,0,1;0rad)
FEATURE [Sketcher::SketchObject] Sketch2420
  MapMode = 5
  Support = -> [XY_Plane995]
  sketch-geometry (8):
    g0: LineSegment StartX=0 StartY=3.17543 StartZ=0 EndX=-2.75 EndY=1.58771 EndZ=0
    g1: LineSegment StartX=-2.75 StartY=1.58771 StartZ=0 EndX=-2.75 EndY=-1.58771 EndZ=0
    g2: LineSegment StartX=-2.75 StartY=-1.58771 StartZ=0 EndX=0 EndY=-3.17543 EndZ=0
    g3: LineSegment StartX=0 StartY=-3.17543 StartZ=0 EndX=2.75 EndY=-1.58771 EndZ=0
    g4: LineSegment StartX=2.75 StartY=-1.58771 StartZ=0 EndX=2.75 EndY=1.58771 EndZ=0
    g5: LineSegment StartX=2.75 StartY=1.58771 StartZ=0 EndX=0 EndY=3.17543 EndZ=0
    g6: Circle [constr] CenterX=0 CenterY=0 CenterZ=0 NormalX=0 NormalY=0 NormalZ=1 AngleXU=0 Radius=3.17543
    g7: Circle CenterX=0 CenterY=0 CenterZ=0 NormalX=0 NormalY=0 NormalZ=1 AngleXU=0 Radius=1.5
  constraints (18):
    c: Coincident(g0,g1)
    c: Coincident(g1,g2)
    c: Coincident(g2,g3)
    c: Coincident(g3,g4)
    c: Coincident(g4,g5)
    c: Coincident(g5,g0)
    c: Equal(g0, g1-g5) x5
    c: PointOnObject(g0,g6)
    c: PointOnObject(g1,g6)
    c: PointOnObject(g2,g6)
    c: PointOnObject(g3,g6)
    c: PointOnObject(g4,g6)
    c: PointOnObject(g5,g6)
    c: Coincident(g6,g-1)
    c: PointOnObject(g5,g-2)
    c: DistanceX(g0,g4) = 5.5
    c: Coincident(g7,g-1)
    c: Radius(g7) = 1.5
FEATURE [PartDesign::Pad] Pad1072  label="M3 Nut Primitive220"
  Length = 1.2
  Length2 = 1.2
  Profile = -> Sketch2420
  Type = 4
FEATURE [Sketcher::SketchObject] Sketch2418
  ExternalGeometry = -> [Pad1072]
  MapMode = 5
  Placement = pos=(0,0,0) rot=(0.57735,0.57735,0.57735;2.0944rad)
  Support = -> [YZ_Plane989]
  sketch-geometry (6):
    g0: LineSegment StartX=-2.67543 StartY=1.2 StartZ=0 EndX=-3.67543 EndY=1.2 EndZ=0
    g1: LineSegment StartX=-3.67543 StartY=1.2 StartZ=0 EndX=-3.67543 EndY=-1.2 EndZ=0
    g2: LineSegment StartX=-3.67543 StartY=-1.2 StartZ=0 EndX=-2.67543 EndY=-1.2 EndZ=0
    g3: LineSegment StartX=-2.67543 StartY=-1.2 StartZ=0 EndX=-3.17543 EndY=-1 EndZ=0
    g4: LineSegment StartX=-3.17543 StartY=-1 StartZ=0 EndX=-3.17543 EndY=1 EndZ=0
    g5: LineSegment StartX=-3.17543 StartY=1 StartZ=0 EndX=-2.67543 EndY=1.2 EndZ=0
  constraints (15):
    c: Horizontal(g0)
    c: Coincident(g0,g1)
    c: Coincident(g1,g2)
    c: Coincident(g2,g3)
    c: Coincident(g3,g4)
    c: Coincident(g4,g5)
    c: Coincident(g5,g0)
    c: Symmetric(g4,g3,g-1)
    c: Symmetric(g0,g2,g-1)
    c: Symmetric(g1,g0,g-1)
    c: DistanceX(g0,g4) = 0.5
    c: DistanceY(g3,g4) = 2
    c: DistanceY(g1,g0) = 2.4
    c: PointOnObject(g3,g-3)
    c: DistanceX(g4,g0) = 0.5
FEATURE [PartDesign::Groove] Groove227  label="M3 Nut Smooth219"
  Angle = 360
  Axis = (-2e-16,3e-16,1)
  Base = (0,0,0)
  BaseFeature = -> Pad1072
  Profile = -> Sketch2418
  ReferenceAxis = -> Sketch2418 [V_Axis]
  Reversed = true
FEATURE [PartDesign::Chamfer] Chamfer536  label="M3 Nut Smooth Hole219"
  Base = -> Groove227 [Edge24,Edge23]
  BaseFeature = -> Groove227
  Size = 0.2
FEATURE [PartDesign::Body] Body697  label="M3 Nut123"
  Group = -> [Sketch2420,Pad1072,Sketch2418,Groove227,Chamfer536]
  Origin = -> Origin996
  Placement = pos=(9e-15,20,15) rot=(0.57735,-0.57735,-0.57735;2.0944rad)
  Tip = -> Chamfer536
FEATURE [Sketcher::SketchObject] Sketch2422
  MapMode = 5
  Support = -> [XY_Plane992]
  sketch-geometry (8):
    g0: LineSegment StartX=0 StartY=3.17543 StartZ=0 EndX=-2.75 EndY=1.58771 EndZ=0
    g1: LineSegment StartX=-2.75 StartY=1.58771 StartZ=0 EndX=-2.75 EndY=-1.58771 EndZ=0
    g2: LineSegment StartX=-2.75 StartY=-1.58771 StartZ=0 EndX=0 EndY=-3.17543 EndZ=0
    g3: LineSegment StartX=0 StartY=-3.17543 StartZ=0 EndX=2.75 EndY=-1.58771 EndZ=0
    g4: LineSegment StartX=2.75 StartY=-1.58771 StartZ=0 EndX=2.75 EndY=1.58771 EndZ=0
    g5: LineSegment StartX=2.75 StartY=1.58771 StartZ=0 EndX=0 EndY=3.17543 EndZ=0
    g6: Circle [constr] CenterX=0 CenterY=0 CenterZ=0 NormalX=0 NormalY=0 NormalZ=1 AngleXU=0 Radius=3.17543
    g7: Circle CenterX=0 CenterY=0 CenterZ=0 NormalX=0 NormalY=0 NormalZ=1 AngleXU=0 Radius=1.5
  constraints (18):
    c: Coincident(g0,g1)
    c: Coincident(g1,g2)
    c: Coincident(g2,g3)
    c: Coincident(g3,g4)
    c: Coincident(g4,g5)
    c: Coincident(g5,g0)
    c: Equal(g0, g1-g5) x5
    c: PointOnObject(g0,g6)
    c: PointOnObject(g1,g6)
    c: PointOnObject(g2,g6)
    c: PointOnObject(g3,g6)
    c: PointOnObject(g4,g6)
    c: PointOnObject(g5,g6)
    c: Coincident(g6,g-1)
    c: PointOnObject(g5,g-2)
    c: DistanceX(g0,g4) = 5.5
    c: Coincident(g7,g-1)
    c: Radius(g7) = 1.5
FEATURE [PartDesign::Pad] Pad1070  label="M3 Nut Primitive218"
  Length = 1.2
  Length2 = 1.2
  Profile = -> Sketch2422
  Type = 4
FEATURE [Sketcher::SketchObject] Sketch2423
  MapMode = 5
  Support = -> [XY_Plane996]
  sketch-geometry (8):
    g0: LineSegment StartX=0 StartY=3.17543 StartZ=0 EndX=-2.75 EndY=1.58771 EndZ=0
    g1: LineSegment StartX=-2.75 StartY=1.58771 StartZ=0 EndX=-2.75 EndY=-1.58771 EndZ=0
    g2: LineSegment StartX=-2.75 StartY=-1.58771 StartZ=0 EndX=0 EndY=-3.17543 EndZ=0
    g3: LineSegment StartX=0 StartY=-3.17543 StartZ=0 EndX=2.75 EndY=-1.58771 EndZ=0
    g4: LineSegment StartX=2.75 StartY=-1.58771 StartZ=0 EndX=2.75 EndY=1.58771 EndZ=0
    g5: LineSegment StartX=2.75 StartY=1.58771 StartZ=0 EndX=0 EndY=3.17543 EndZ=0
    g6: Circle [constr] CenterX=0 CenterY=0 CenterZ=0 NormalX=0 NormalY=0 NormalZ=1 AngleXU=0 Radius=3.17543
    g7: Circle CenterX=0 CenterY=0 CenterZ=0 NormalX=0 NormalY=0 NormalZ=1 AngleXU=0 Radius=1.5
  constraints (18):
    c: Coincident(g0,g1)
    c: Coincident(g1,g2)
    c: Coincident(g2,g3)
    c: Coincident(g3,g4)
    c: Coincident(g4,g5)
    c: Coincident(g5,g0)
    c: Equal(g0, g1-g5) x5
    c: PointOnObject(g0,g6)
    c: PointOnObject(g1,g6)
    c: PointOnObject(g2,g6)
    c: PointOnObject(g3,g6)
    c: PointOnObject(g4,g6)
    c: PointOnObject(g5,g6)
    c: Coincident(g6,g-1)
    c: PointOnObject(g5,g-2)
    c: DistanceX(g0,g4) = 5.5
    c: Coincident(g7,g-1)
    c: Radius(g7) = 1.5
FEATURE [PartDesign::Pad] Pad1069  label="M3 Nut Primitive217"
  Length = 1.2
  Length2 = 1.2
  Profile = -> Sketch2423
  Type = 4
FEATURE [Sketcher::SketchObject] Sketch2421
  ExternalGeometry = -> [Pad1069]
  MapMode = 5
  Placement = pos=(0,0,0) rot=(0.57735,0.57735,0.57735;2.0944rad)
  Support = -> [YZ_Plane990]
  sketch-geometry (6):
    g0: LineSegment StartX=-2.67543 StartY=1.2 StartZ=0 EndX=-3.67543 EndY=1.2 EndZ=0
    g1: LineSegment StartX=-3.67543 StartY=1.2 StartZ=0 EndX=-3.67543 EndY=-1.2 EndZ=0
    g2: LineSegment StartX=-3.67543 StartY=-1.2 StartZ=0 EndX=-2.67543 EndY=-1.2 EndZ=0
    g3: LineSegment StartX=-2.67543 StartY=-1.2 StartZ=0 EndX=-3.17543 EndY=-1 EndZ=0
    g4: LineSegment StartX=-3.17543 StartY=-1 StartZ=0 EndX=-3.17543 EndY=1 EndZ=0
    g5: LineSegment StartX=-3.17543 StartY=1 StartZ=0 EndX=-2.67543 EndY=1.2 EndZ=0
  constraints (15):
    c: Horizontal(g0)
    c: Coincident(g0,g1)
    c: Coincident(g1,g2)
    c: Coincident(g2,g3)
    c: Coincident(g3,g4)
    c: Coincident(g4,g5)
    c: Coincident(g5,g0)
    c: Symmetric(g4,g3,g-1)
    c: Symmetric(g0,g2,g-1)
    c: Symmetric(g1,g0,g-1)
    c: DistanceX(g0,g4) = 0.5
    c: DistanceY(g3,g4) = 2
    c: DistanceY(g1,g0) = 2.4
    c: PointOnObject(g3,g-3)
    c: DistanceX(g4,g0) = 0.5
FEATURE [PartDesign::Groove] Groove225  label="M3 Nut Smooth217"
  Angle = 360
  Axis = (-2e-16,3e-16,1)
  Base = (0,0,0)
  BaseFeature = -> Pad1069
  Profile = -> Sketch2421
  ReferenceAxis = -> Sketch2421 [V_Axis]
  Reversed = true
FEATURE [PartDesign::Chamfer] Chamfer535  label="M3 Nut Smooth Hole218"
  Base = -> Groove225 [Edge24,Edge23]
  BaseFeature = -> Groove225
  Size = 0.2
FEATURE [PartDesign::Body] Body698  label="M3 Nut124"
  Group = -> [Sketch2423,Pad1069,Sketch2421,Groove225,Chamfer535]
  Origin = -> Origin997
  Placement = pos=(0,-1.6e-14,73.25) rot=(0.57735,-0.57735,-0.57735;2.0944rad)
  Tip = -> Chamfer535
FEATURE [Sketcher::SketchObject] Sketch2424
  ExternalGeometry = -> [Pad1070]
  MapMode = 5
  Placement = pos=(0,0,0) rot=(0.57735,0.57735,0.57735;2.0944rad)
  Support = -> [YZ_Plane986]
  sketch-geometry (6):
    g0: LineSegment StartX=-2.67543 StartY=1.2 StartZ=0 EndX=-3.67543 EndY=1.2 EndZ=0
    g1: LineSegment StartX=-3.67543 StartY=1.2 StartZ=0 EndX=-3.67543 EndY=-1.2 EndZ=0
    g2: LineSegment StartX=-3.67543 StartY=-1.2 StartZ=0 EndX=-2.67543 EndY=-1.2 EndZ=0
    g3: LineSegment StartX=-2.67543 StartY=-1.2 StartZ=0 EndX=-3.17543 EndY=-1 EndZ=0
    g4: LineSegment StartX=-3.17543 StartY=-1 StartZ=0 EndX=-3.17543 EndY=1 EndZ=0
    g5: LineSegment StartX=-3.17543 StartY=1 StartZ=0 EndX=-2.67543 EndY=1.2 EndZ=0
  constraints (15):
    c: Horizontal(g0)
    c: Coincident(g0,g1)
    c: Coincident(g1,g2)
    c: Coincident(g2,g3)
    c: Coincident(g3,g4)
    c: Coincident(g4,g5)
    c: Coincident(g5,g0)
    c: Symmetric(g4,g3,g-1)
    c: Symmetric(g0,g2,g-1)
    c: Symmetric(g1,g0,g-1)
    c: DistanceX(g0,g4) = 0.5
    c: DistanceY(g3,g4) = 2
    c: DistanceY(g1,g0) = 2.4
    c: PointOnObject(g3,g-3)
    c: DistanceX(g4,g0) = 0.5
FEATURE [PartDesign::Groove] Groove228  label="M3 Nut Smooth220"
  Angle = 360
  Axis = (-2e-16,3e-16,1)
  Base = (0,0,0)
  BaseFeature = -> Pad1070
  Profile = -> Sketch2424
  ReferenceAxis = -> Sketch2424 [V_Axis]
  Reversed = true
FEATURE [PartDesign::Chamfer] Chamfer534  label="M3 Nut Smooth Hole217"
  Base = -> Groove228 [Edge24,Edge23]
  BaseFeature = -> Groove228
  Size = 0.2
FEATURE [PartDesign::Body] Body695  label="M3 Nut121"
  Group = -> [Sketch2422,Pad1070,Sketch2424,Groove228,Chamfer534]
  Origin = -> Origin994
  Placement = pos=(1.3e-14,30,73.25) rot=(0.57735,-0.57735,-0.57735;2.0944rad)
  Tip = -> Chamfer534
FEATURE [Sketcher::SketchObject] Sketch2425
  MapMode = 5
  Support = -> [XY_Plane994]
  sketch-geometry (8):
    g0: LineSegment StartX=0 StartY=3.17543 StartZ=0 EndX=-2.75 EndY=1.58771 EndZ=0
    g1: LineSegment StartX=-2.75 StartY=1.58771 StartZ=0 EndX=-2.75 EndY=-1.58771 EndZ=0
    g2: LineSegment StartX=-2.75 StartY=-1.58771 StartZ=0 EndX=0 EndY=-3.17543 EndZ=0
    g3: LineSegment StartX=0 StartY=-3.17543 StartZ=0 EndX=2.75 EndY=-1.58771 EndZ=0
    g4: LineSegment StartX=2.75 StartY=-1.58771 StartZ=0 EndX=2.75 EndY=1.58771 EndZ=0
    g5: LineSegment StartX=2.75 StartY=1.58771 StartZ=0 EndX=0 EndY=3.17543 EndZ=0
    g6: Circle [constr] CenterX=0 CenterY=0 CenterZ=0 NormalX=0 NormalY=0 NormalZ=1 AngleXU=0 Radius=3.17543
    g7: Circle CenterX=0 CenterY=0 CenterZ=0 NormalX=0 NormalY=0 NormalZ=1 AngleXU=0 Radius=1.5
  constraints (18):
    c: Coincident(g0,g1)
    c: Coincident(g1,g2)
    c: Coincident(g2,g3)
    c: Coincident(g3,g4)
    c: Coincident(g4,g5)
    c: Coincident(g5,g0)
    c: Equal(g0, g1-g5) x5
    c: PointOnObject(g0,g6)
    c: PointOnObject(g1,g6)
    c: PointOnObject(g2,g6)
    c: PointOnObject(g3,g6)
    c: PointOnObject(g4,g6)
    c: PointOnObject(g5,g6)
    c: Coincident(g6,g-1)
    c: PointOnObject(g5,g-2)
    c: DistanceX(g0,g4) = 5.5
    c: Coincident(g7,g-1)
    c: Radius(g7) = 1.5
FEATURE [PartDesign::Pad] Pad1071  label="M3 Nut Primitive219"
  Length = 1.2
  Length2 = 1.2
  Profile = -> Sketch2425
  Type = 4
FEATURE [Sketcher::SketchObject] Sketch2419
  ExternalGeometry = -> [Pad1071]
  MapMode = 5
  Placement = pos=(0,0,0) rot=(0.57735,0.57735,0.57735;2.0944rad)
  Support = -> [YZ_Plane988]
  sketch-geometry (6):
    g0: LineSegment StartX=-2.67543 StartY=1.2 StartZ=0 EndX=-3.67543 EndY=1.2 EndZ=0
    g1: LineSegment StartX=-3.67543 StartY=1.2 StartZ=0 EndX=-3.67543 EndY=-1.2 EndZ=0
    g2: LineSegment StartX=-3.67543 StartY=-1.2 StartZ=0 EndX=-2.67543 EndY=-1.2 EndZ=0
    g3: LineSegment StartX=-2.67543 StartY=-1.2 StartZ=0 EndX=-3.17543 EndY=-1 EndZ=0
    g4: LineSegment StartX=-3.17543 StartY=-1 StartZ=0 EndX=-3.17543 EndY=1 EndZ=0
    g5: LineSegment StartX=-3.17543 StartY=1 StartZ=0 EndX=-2.67543 EndY=1.2 EndZ=0
  constraints (15):
    c: Horizontal(g0)
    c: Coincident(g0,g1)
    c: Coincident(g1,g2)
    c: Coincident(g2,g3)
    c: Coincident(g3,g4)
    c: Coincident(g4,g5)
    c: Coincident(g5,g0)
    c: Symmetric(g4,g3,g-1)
    c: Symmetric(g0,g2,g-1)
    c: Symmetric(g1,g0,g-1)
    c: DistanceX(g0,g4) = 0.5
    c: DistanceY(g3,g4) = 2
    c: DistanceY(g1,g0) = 2.4
    c: PointOnObject(g3,g-3)
    c: DistanceX(g4,g0) = 0.5
FEATURE [PartDesign::Groove] Groove226  label="M3 Nut Smooth218"
  Angle = 360
  Axis = (-2e-16,3e-16,1)
  Base = (0,0,0)
  BaseFeature = -> Pad1071
  Profile = -> Sketch2419
  ReferenceAxis = -> Sketch2419 [V_Axis]
  Reversed = true
FEATURE [PartDesign::Chamfer] Chamfer537  label="M3 Nut Smooth Hole220"
  Base = -> Groove226 [Edge24,Edge23]
  BaseFeature = -> Groove226
  Size = 0.2
FEATURE [PartDesign::Body] Body696  label="M3 Nut122"
  Group = -> [Sketch2425,Pad1071,Sketch2419,Groove226,Chamfer537]
  Origin = -> Origin995
  Placement = pos=(4e-15,10,15) rot=(0.57735,-0.57735,-0.57735;2.0944rad)
  Tip = -> Chamfer537
FEATURE [App::Part] Part275  label="Rear Shoulder Nuts"
  Group = -> [Body698,Body695,Body696,Body697]
  Origin = -> Origin998
  Placement = pos=(-231.25,-85,157.5) rot=(0,0,1;3.14159rad)
FEATURE [Sketcher::SketchObject] Sketch2428
  MapMode = 5
  Support = -> [XY_Plane997]
  sketch-geometry (1):
    g0: Circle CenterX=0 CenterY=0 CenterZ=0 NormalX=0 NormalY=0 NormalZ=1 AngleXU=0 Radius=2.75
  constraints (2):
    c: Coincident(g0,g-1)
    c: Radius(g0) = 2.75
FEATURE [PartDesign::Pad] Pad1073  label="M3x8 Head163"
  Length = 3
  Length2 = 100
  Profile = -> Sketch2428
  Type = 0
FEATURE [Sketcher::SketchObject] Sketch2427
  MapMode = 5
  Placement = pos=(0,0,3) rot=(0,0,1;0rad)
  Support = -> [Pad1073]
  sketch-geometry (1):
    g0: Circle CenterX=0 CenterY=0 CenterZ=0 NormalX=0 NormalY=0 NormalZ=1 AngleXU=0 Radius=1.5
  constraints (2):
    c: Coincident(g0,g-1)
    c: Radius(g0) = 1.5
FEATURE [PartDesign::Pad] Pad1074  label="M3x8 Thread163"
  BaseFeature = -> Pad1073
  Length = 8
  Length2 = 100
  Profile = -> Sketch2427
  Type = 0
FEATURE [Sketcher::SketchObject] Sketch2426
  MapMode = 5
  Placement = pos=(0,0,0) rot=(1,0,0;3.14159rad)
  Support = -> [Pad1074]
  sketch-geometry (7):
    g0: LineSegment StartX=1.275 StartY=0.736122 StartZ=0 EndX=0 EndY=1.47224 EndZ=0
    g1: LineSegment StartX=0 StartY=1.47224 StartZ=0 EndX=-1.275 EndY=0.736122 EndZ=0
    g2: LineSegment StartX=-1.275 StartY=0.736122 StartZ=0 EndX=-1.275 EndY=-0.736122 EndZ=0
    g3: LineSegment StartX=-1.275 StartY=-0.736122 StartZ=0 EndX=1.34766e-11 EndY=-1.47224 EndZ=0
    g4: LineSegment StartX=1.34766e-11 StartY=-1.47224 StartZ=0 EndX=1.275 EndY=-0.736122 EndZ=0
    g5: LineSegment StartX=1.275 StartY=-0.736122 StartZ=0 EndX=1.275 EndY=0.736122 EndZ=0
    g6: Circle [constr] CenterX=0 CenterY=0 CenterZ=0 NormalX=0 NormalY=0 NormalZ=1 AngleXU=0 Radius=1.47224
  constraints (16):
    c: Coincident(g0,g1)
    c: Coincident(g1,g2)
    c: Coincident(g2,g3)
    c: Coincident(g3,g4)
    c: Coincident(g4,g5)
    c: Coincident(g5,g0)
    c: Equal(g0, g1-g5) x5
    c: PointOnObject(g0,g6)
    c: PointOnObject(g1,g6)
    c: PointOnObject(g2,g6)
    c: PointOnObject(g3,g6)
    c: PointOnObject(g4,g6)
    c: PointOnObject(g5,g6)
    c: Coincident(g6,g-1)
    c: PointOnObject(g0,g-2)
    c: DistanceX(g1,g0) = 2.55
FEATURE [PartDesign::Pocket] Pocket857  label="M3x8 Wrench163"
  BaseFeature = -> Pad1074
  Length = 1.3
  Length2 = 100
  Profile = -> Sketch2426
  Type = 0
FEATURE [PartDesign::Chamfer] Chamfer538  label="M3x8 Smooth162"
  Base = -> Pocket857 [Face11,Edge2,Edge24,Edge3]
  BaseFeature = -> Pocket857
  Size = 0.2
FEATURE [PartDesign::Body] Body699  label="M3x135"
  Group = -> [Sketch2428,Pad1073,Sketch2427,Pad1074,Sketch2426,Pocket857,Chamfer538]
  Origin = -> Origin999
  Placement = pos=(0,0,0) rot=(0,1,0;4.71239rad)
  Tip = -> Chamfer538
FEATURE [Sketcher::SketchObject] Sketch2431
  MapMode = 5
  Support = -> [XY_Plane998]
  sketch-geometry (1):
    g0: Circle CenterX=0 CenterY=0 CenterZ=0 NormalX=0 NormalY=0 NormalZ=1 AngleXU=0 Radius=2.75
  constraints (2):
    c: Coincident(g0,g-1)
    c: Radius(g0) = 2.75
FEATURE [PartDesign::Pad] Pad1075  label="M3x8 Head164"
  Length = 3
  Length2 = 100
  Profile = -> Sketch2431
  Type = 0
FEATURE [Sketcher::SketchObject] Sketch2430
  MapMode = 5
  Placement = pos=(0,0,3) rot=(0,0,1;0rad)
  Support = -> [Pad1075]
  sketch-geometry (1):
    g0: Circle CenterX=0 CenterY=0 CenterZ=0 NormalX=0 NormalY=0 NormalZ=1 AngleXU=0 Radius=1.5
  constraints (2):
    c: Coincident(g0,g-1)
    c: Radius(g0) = 1.5
FEATURE [PartDesign::Pad] Pad1076  label="M3x8 Thread164"
  BaseFeature = -> Pad1075
  Length = 8
  Length2 = 100
  Profile = -> Sketch2430
  Type = 0
FEATURE [Sketcher::SketchObject] Sketch2429
  MapMode = 5
  Placement = pos=(0,0,0) rot=(1,0,0;3.14159rad)
  Support = -> [Pad1076]
  sketch-geometry (7):
    g0: LineSegment StartX=1.275 StartY=0.736122 StartZ=0 EndX=0 EndY=1.47224 EndZ=0
    g1: LineSegment StartX=0 StartY=1.47224 StartZ=0 EndX=-1.275 EndY=0.736122 EndZ=0
    g2: LineSegment StartX=-1.275 StartY=0.736122 StartZ=0 EndX=-1.275 EndY=-0.736122 EndZ=0
    g3: LineSegment StartX=-1.275 StartY=-0.736122 StartZ=0 EndX=1.34766e-11 EndY=-1.47224 EndZ=0
    g4: LineSegment StartX=1.34766e-11 StartY=-1.47224 StartZ=0 EndX=1.275 EndY=-0.736122 EndZ=0
    g5: LineSegment StartX=1.275 StartY=-0.736122 StartZ=0 EndX=1.275 EndY=0.736122 EndZ=0
    g6: Circle [constr] CenterX=0 CenterY=0 CenterZ=0 NormalX=0 NormalY=0 NormalZ=1 AngleXU=0 Radius=1.47224
  constraints (16):
    c: Coincident(g0,g1)
    c: Coincident(g1,g2)
    c: Coincident(g2,g3)
    c: Coincident(g3,g4)
    c: Coincident(g4,g5)
    c: Coincident(g5,g0)
    c: Equal(g0, g1-g5) x5
    c: PointOnObject(g0,g6)
    c: PointOnObject(g1,g6)
    c: PointOnObject(g2,g6)
    c: PointOnObject(g3,g6)
    c: PointOnObject(g4,g6)
    c: PointOnObject(g5,g6)
    c: Coincident(g6,g-1)
    c: PointOnObject(g0,g-2)
    c: DistanceX(g1,g0) = 2.55
FEATURE [PartDesign::Pocket] Pocket858  label="M3x8 Wrench164"
  BaseFeature = -> Pad1076
  Length = 1.3
  Length2 = 100
  Profile = -> Sketch2429
  Type = 0
FEATURE [PartDesign::Chamfer] Chamfer539  label="M3x8 Smooth163"
  Base = -> Pocket858 [Face11,Edge2,Edge24,Edge3]
  BaseFeature = -> Pocket858
  Size = 0.2
FEATURE [PartDesign::Body] Body700  label="M3x136"
  Group = -> [Sketch2431,Pad1075,Sketch2430,Pad1076,Sketch2429,Pocket858,Chamfer539]
  Origin = -> Origin1000
  Placement = pos=(0,10,0) rot=(0,1,0;4.71239rad)
  Tip = -> Chamfer539
FEATURE [Sketcher::SketchObject] Sketch2434
  MapMode = 5
  Support = -> [XY_Plane999]
  sketch-geometry (1):
    g0: Circle CenterX=0 CenterY=0 CenterZ=0 NormalX=0 NormalY=0 NormalZ=1 AngleXU=0 Radius=2.75
  constraints (2):
    c: Coincident(g0,g-1)
    c: Radius(g0) = 2.75
FEATURE [PartDesign::Pad] Pad1077  label="M3x8 Head165"
  Length = 3
  Length2 = 100
  Profile = -> Sketch2434
  Type = 0
FEATURE [Sketcher::SketchObject] Sketch2433
  MapMode = 5
  Placement = pos=(0,0,3) rot=(0,0,1;0rad)
  Support = -> [Pad1077]
  sketch-geometry (1):
    g0: Circle CenterX=0 CenterY=0 CenterZ=0 NormalX=0 NormalY=0 NormalZ=1 AngleXU=0 Radius=1.5
  constraints (2):
    c: Coincident(g0,g-1)
    c: Radius(g0) = 1.5
FEATURE [PartDesign::Pad] Pad1078  label="M3x8 Thread165"
  BaseFeature = -> Pad1077
  Length = 8
  Length2 = 100
  Profile = -> Sketch2433
  Type = 0
FEATURE [Sketcher::SketchObject] Sketch2432
  MapMode = 5
  Placement = pos=(0,0,0) rot=(1,0,0;3.14159rad)
  Support = -> [Pad1078]
  sketch-geometry (7):
    g0: LineSegment StartX=1.275 StartY=0.736122 StartZ=0 EndX=0 EndY=1.47224 EndZ=0
    g1: LineSegment StartX=0 StartY=1.47224 StartZ=0 EndX=-1.275 EndY=0.736122 EndZ=0
    g2: LineSegment StartX=-1.275 StartY=0.736122 StartZ=0 EndX=-1.275 EndY=-0.736122 EndZ=0
    g3: LineSegment StartX=-1.275 StartY=-0.736122 StartZ=0 EndX=1.34766e-11 EndY=-1.47224 EndZ=0
    g4: LineSegment StartX=1.34766e-11 StartY=-1.47224 StartZ=0 EndX=1.275 EndY=-0.736122 EndZ=0
    g5: LineSegment StartX=1.275 StartY=-0.736122 StartZ=0 EndX=1.275 EndY=0.736122 EndZ=0
    g6: Circle [constr] CenterX=0 CenterY=0 CenterZ=0 NormalX=0 NormalY=0 NormalZ=1 AngleXU=0 Radius=1.47224
  constraints (16):
    c: Coincident(g0,g1)
    c: Coincident(g1,g2)
    c: Coincident(g2,g3)
    c: Coincident(g3,g4)
    c: Coincident(g4,g5)
    c: Coincident(g5,g0)
    c: Equal(g0, g1-g5) x5
    c: PointOnObject(g0,g6)
    c: PointOnObject(g1,g6)
    c: PointOnObject(g2,g6)
    c: PointOnObject(g3,g6)
    c: PointOnObject(g4,g6)
    c: PointOnObject(g5,g6)
    c: Coincident(g6,g-1)
    c: PointOnObject(g0,g-2)
    c: DistanceX(g1,g0) = 2.55
FEATURE [PartDesign::Pocket] Pocket859  label="M3x8 Wrench165"
  BaseFeature = -> Pad1078
  Length = 1.3
  Length2 = 100
  Profile = -> Sketch2432
  Type = 0
FEATURE [PartDesign::Chamfer] Chamfer540  label="M3x8 Smooth164"
  Base = -> Pocket859 [Face11,Edge2,Edge24,Edge3]
  BaseFeature = -> Pocket859
  Size = 0.2
FEATURE [PartDesign::Body] Body701  label="M3x137"
  Group = -> [Sketch2434,Pad1077,Sketch2433,Pad1078,Sketch2432,Pocket859,Chamfer540]
  Origin = -> Origin1001
  Placement = pos=(-1.29e-14,-10,58) rot=(0,1,0;4.71239rad)
  Tip = -> Chamfer540
FEATURE [Sketcher::SketchObject] Sketch2437
  MapMode = 5
  Support = -> [XY_Plane1000]
  sketch-geometry (1):
    g0: Circle CenterX=0 CenterY=0 CenterZ=0 NormalX=0 NormalY=0 NormalZ=1 AngleXU=0 Radius=2.75
  constraints (2):
    c: Coincident(g0,g-1)
    c: Radius(g0) = 2.75
FEATURE [PartDesign::Pad] Pad1079  label="M3x8 Head166"
  Length = 3
  Length2 = 100
  Profile = -> Sketch2437
  Type = 0
FEATURE [Sketcher::SketchObject] Sketch2436
  MapMode = 5
  Placement = pos=(0,0,3) rot=(0,0,1;0rad)
  Support = -> [Pad1079]
  sketch-geometry (1):
    g0: Circle CenterX=0 CenterY=0 CenterZ=0 NormalX=0 NormalY=0 NormalZ=1 AngleXU=0 Radius=1.5
  constraints (2):
    c: Coincident(g0,g-1)
    c: Radius(g0) = 1.5
FEATURE [PartDesign::Pad] Pad1080  label="M3x8 Thread166"
  BaseFeature = -> Pad1079
  Length = 8
  Length2 = 100
  Profile = -> Sketch2436
  Type = 0
FEATURE [Sketcher::SketchObject] Sketch2435
  MapMode = 5
  Placement = pos=(0,0,0) rot=(1,0,0;3.14159rad)
  Support = -> [Pad1080]
  sketch-geometry (7):
    g0: LineSegment StartX=1.275 StartY=0.736122 StartZ=0 EndX=0 EndY=1.47224 EndZ=0
    g1: LineSegment StartX=0 StartY=1.47224 StartZ=0 EndX=-1.275 EndY=0.736122 EndZ=0
    g2: LineSegment StartX=-1.275 StartY=0.736122 StartZ=0 EndX=-1.275 EndY=-0.736122 EndZ=0
    g3: LineSegment StartX=-1.275 StartY=-0.736122 StartZ=0 EndX=1.34766e-11 EndY=-1.47224 EndZ=0
    g4: LineSegment StartX=1.34766e-11 StartY=-1.47224 StartZ=0 EndX=1.275 EndY=-0.736122 EndZ=0
    g5: LineSegment StartX=1.275 StartY=-0.736122 StartZ=0 EndX=1.275 EndY=0.736122 EndZ=0
    g6: Circle [constr] CenterX=0 CenterY=0 CenterZ=0 NormalX=0 NormalY=0 NormalZ=1 AngleXU=0 Radius=1.47224
  constraints (16):
    c: Coincident(g0,g1)
    c: Coincident(g1,g2)
    c: Coincident(g2,g3)
    c: Coincident(g3,g4)
    c: Coincident(g4,g5)
    c: Coincident(g5,g0)
    c: Equal(g0, g1-g5) x5
    c: PointOnObject(g0,g6)
    c: PointOnObject(g1,g6)
    c: PointOnObject(g2,g6)
    c: PointOnObject(g3,g6)
    c: PointOnObject(g4,g6)
    c: PointOnObject(g5,g6)
    c: Coincident(g6,g-1)
    c: PointOnObject(g0,g-2)
    c: DistanceX(g1,g0) = 2.55
FEATURE [PartDesign::Pocket] Pocket860  label="M3x8 Wrench166"
  BaseFeature = -> Pad1080
  Length = 1.3
  Length2 = 100
  Profile = -> Sketch2435
  Type = 0
FEATURE [PartDesign::Chamfer] Chamfer541  label="M3x8 Smooth165"
  Base = -> Pocket860 [Face11,Edge2,Edge24,Edge3]
  BaseFeature = -> Pocket860
  Size = 0.2
FEATURE [PartDesign::Body] Body702  label="M3x138"
  Group = -> [Sketch2437,Pad1079,Sketch2436,Pad1080,Sketch2435,Pocket860,Chamfer541]
  Origin = -> Origin1002
  Placement = pos=(-1.29e-14,20,58.05) rot=(0,1,0;4.71239rad)
  Tip = -> Chamfer541
FEATURE [App::Part] Part276  label="Front Shoulder Screws"
  Group = -> [Body699,Body700,Body701,Body702]
  Origin = -> Origin1003
  Placement = pos=(24.4,-104.9,172.35) rot=(0,0,1;0rad)
FEATURE [App::Part] Part268  label="Front Legs and Shoulder"
  Group = -> [Part,Part151,Part223,Part272,Part273,Part274,Part276]
  Origin = -> Origin971
  Placement = pos=(0.25,-0.25,-0.25) rot=(0,0,1;0rad)
FEATURE [Sketcher::SketchObject] Sketch2441
  MapMode = 5
  Support = -> [XY_Plane1004]
  sketch-geometry (1):
    g0: Circle CenterX=0 CenterY=0 CenterZ=0 NormalX=0 NormalY=0 NormalZ=1 AngleXU=0 Radius=2.75
  constraints (2):
    c: Coincident(g0,g-1)
    c: Radius(g0) = 2.75
FEATURE [PartDesign::Pad] Pad1088  label="M3x8 Head170"
  Length = 3
  Length2 = 100
  Profile = -> Sketch2441
  Type = 0
FEATURE [Sketcher::SketchObject] Sketch2442
  MapMode = 5
  Placement = pos=(0,0,3) rot=(0,0,1;0rad)
  Support = -> [Pad1088]
  sketch-geometry (1):
    g0: Circle CenterX=0 CenterY=0 CenterZ=0 NormalX=0 NormalY=0 NormalZ=1 AngleXU=0 Radius=1.5
  constraints (2):
    c: Coincident(g0,g-1)
    c: Radius(g0) = 1.5
FEATURE [PartDesign::Pad] Pad1087  label="M3x8 Thread170"
  BaseFeature = -> Pad1088
  Length = 8
  Length2 = 100
  Profile = -> Sketch2442
  Type = 0
FEATURE [Sketcher::SketchObject] Sketch2440
  MapMode = 5
  Placement = pos=(0,0,0) rot=(1,0,0;3.14159rad)
  Support = -> [Pad1087]
  sketch-geometry (7):
    g0: LineSegment StartX=1.275 StartY=0.736122 StartZ=0 EndX=0 EndY=1.47224 EndZ=0
    g1: LineSegment StartX=0 StartY=1.47224 StartZ=0 EndX=-1.275 EndY=0.736122 EndZ=0
    g2: LineSegment StartX=-1.275 StartY=0.736122 StartZ=0 EndX=-1.275 EndY=-0.736122 EndZ=0
    g3: LineSegment StartX=-1.275 StartY=-0.736122 StartZ=0 EndX=1.34766e-11 EndY=-1.47224 EndZ=0
    g4: LineSegment StartX=1.34766e-11 StartY=-1.47224 StartZ=0 EndX=1.275 EndY=-0.736122 EndZ=0
    g5: LineSegment StartX=1.275 StartY=-0.736122 StartZ=0 EndX=1.275 EndY=0.736122 EndZ=0
    g6: Circle [constr] CenterX=0 CenterY=0 CenterZ=0 NormalX=0 NormalY=0 NormalZ=1 AngleXU=0 Radius=1.47224
  constraints (16):
    c: Coincident(g0,g1)
    c: Coincident(g1,g2)
    c: Coincident(g2,g3)
    c: Coincident(g3,g4)
    c: Coincident(g4,g5)
    c: Coincident(g5,g0)
    c: Equal(g0, g1-g5) x5
    c: PointOnObject(g0,g6)
    c: PointOnObject(g1,g6)
    c: PointOnObject(g2,g6)
    c: PointOnObject(g3,g6)
    c: PointOnObject(g4,g6)
    c: PointOnObject(g5,g6)
    c: Coincident(g6,g-1)
    c: PointOnObject(g0,g-2)
    c: DistanceX(g1,g0) = 2.55
FEATURE [PartDesign::Pocket] Pocket864  label="M3x8 Wrench170"
  BaseFeature = -> Pad1087
  Length = 1.3
  Length2 = 100
  Profile = -> Sketch2440
  Type = 0
FEATURE [PartDesign::Chamfer] Chamfer543  label="M3x8 Smooth167"
  Base = -> Pocket864 [Face11,Edge2,Edge24,Edge3]
  BaseFeature = -> Pocket864
  Size = 0.2
FEATURE [PartDesign::Body] Body703  label="M3x139"
  Group = -> [Sketch2441,Pad1088,Sketch2442,Pad1087,Sketch2440,Pocket864,Chamfer543]
  Origin = -> Origin1006
  Placement = pos=(0,0,0) rot=(0,-1,0;1.5708rad)
  Tip = -> Chamfer543
FEATURE [Sketcher::SketchObject] Sketch2444
  MapMode = 5
  Support = -> [XY_Plane1005]
  sketch-geometry (1):
    g0: Circle CenterX=0 CenterY=0 CenterZ=0 NormalX=0 NormalY=0 NormalZ=1 AngleXU=0 Radius=2.75
  constraints (2):
    c: Coincident(g0,g-1)
    c: Radius(g0) = 2.75
FEATURE [PartDesign::Pad] Pad1083  label="M3x8 Head168"
  Length = 3
  Length2 = 100
  Profile = -> Sketch2444
  Type = 0
FEATURE [Sketcher::SketchObject] Sketch2443
  MapMode = 5
  Placement = pos=(0,0,3) rot=(0,0,1;0rad)
  Support = -> [Pad1083]
  sketch-geometry (1):
    g0: Circle CenterX=0 CenterY=0 CenterZ=0 NormalX=0 NormalY=0 NormalZ=1 AngleXU=0 Radius=1.5
  constraints (2):
    c: Coincident(g0,g-1)
    c: Radius(g0) = 1.5
FEATURE [PartDesign::Pad] Pad1084  label="M3x8 Thread168"
  BaseFeature = -> Pad1083
  Length = 8
  Length2 = 100
  Profile = -> Sketch2443
  Type = 0
FEATURE [Sketcher::SketchObject] Sketch2438
  MapMode = 5
  Placement = pos=(0,0,0) rot=(1,0,0;3.14159rad)
  Support = -> [Pad1084]
  sketch-geometry (7):
    g0: LineSegment StartX=1.275 StartY=0.736122 StartZ=0 EndX=0 EndY=1.47224 EndZ=0
    g1: LineSegment StartX=0 StartY=1.47224 StartZ=0 EndX=-1.275 EndY=0.736122 EndZ=0
    g2: LineSegment StartX=-1.275 StartY=0.736122 StartZ=0 EndX=-1.275 EndY=-0.736122 EndZ=0
    g3: LineSegment StartX=-1.275 StartY=-0.736122 StartZ=0 EndX=1.34766e-11 EndY=-1.47224 EndZ=0
    g4: LineSegment StartX=1.34766e-11 StartY=-1.47224 StartZ=0 EndX=1.275 EndY=-0.736122 EndZ=0
    g5: LineSegment StartX=1.275 StartY=-0.736122 StartZ=0 EndX=1.275 EndY=0.736122 EndZ=0
    g6: Circle [constr] CenterX=0 CenterY=0 CenterZ=0 NormalX=0 NormalY=0 NormalZ=1 AngleXU=0 Radius=1.47224
  constraints (16):
    c: Coincident(g0,g1)
    c: Coincident(g1,g2)
    c: Coincident(g2,g3)
    c: Coincident(g3,g4)
    c: Coincident(g4,g5)
    c: Coincident(g5,g0)
    c: Equal(g0, g1-g5) x5
    c: PointOnObject(g0,g6)
    c: PointOnObject(g1,g6)
    c: PointOnObject(g2,g6)
    c: PointOnObject(g3,g6)
    c: PointOnObject(g4,g6)
    c: PointOnObject(g5,g6)
    c: Coincident(g6,g-1)
    c: PointOnObject(g0,g-2)
    c: DistanceX(g1,g0) = 2.55
FEATURE [PartDesign::Pocket] Pocket863  label="M3x8 Wrench169"
  BaseFeature = -> Pad1084
  Length = 1.3
  Length2 = 100
  Profile = -> Sketch2438
  Type = 0
FEATURE [PartDesign::Chamfer] Chamfer544  label="M3x8 Smooth168"
  Base = -> Pocket863 [Face11,Edge2,Edge24,Edge3]
  BaseFeature = -> Pocket863
  Size = 0.2
FEATURE [PartDesign::Body] Body705  label="M3x141"
  Group = -> [Sketch2444,Pad1083,Sketch2443,Pad1084,Sketch2438,Pocket863,Chamfer544]
  Origin = -> Origin1005
  Placement = pos=(0,10,0) rot=(0,-1,0;1.5708rad)
  Tip = -> Chamfer544
FEATURE [Sketcher::SketchObject] Sketch2447
  MapMode = 5
  Support = -> [XY_Plane1006]
  sketch-geometry (1):
    g0: Circle CenterX=0 CenterY=0 CenterZ=0 NormalX=0 NormalY=0 NormalZ=1 AngleXU=0 Radius=2.75
  constraints (2):
    c: Coincident(g0,g-1)
    c: Radius(g0) = 2.75
FEATURE [PartDesign::Pad] Pad1085  label="M3x8 Head169"
  Length = 3
  Length2 = 100
  Profile = -> Sketch2447
  Type = 0
FEATURE [Sketcher::SketchObject] Sketch2448
  MapMode = 5
  Support = -> [XY_Plane1003]
  sketch-geometry (1):
    g0: Circle CenterX=0 CenterY=0 CenterZ=0 NormalX=0 NormalY=0 NormalZ=1 AngleXU=0 Radius=2.75
  constraints (2):
    c: Coincident(g0,g-1)
    c: Radius(g0) = 2.75
FEATURE [PartDesign::Pad] Pad1082  label="M3x8 Head167"
  Length = 3
  Length2 = 100
  Profile = -> Sketch2448
  Type = 0
FEATURE [Sketcher::SketchObject] Sketch2445
  MapMode = 5
  Placement = pos=(0,0,3) rot=(0,0,1;0rad)
  Support = -> [Pad1082]
  sketch-geometry (1):
    g0: Circle CenterX=0 CenterY=0 CenterZ=0 NormalX=0 NormalY=0 NormalZ=1 AngleXU=0 Radius=1.5
  constraints (2):
    c: Coincident(g0,g-1)
    c: Radius(g0) = 1.5
FEATURE [PartDesign::Pad] Pad1086  label="M3x8 Thread169"
  BaseFeature = -> Pad1082
  Length = 8
  Length2 = 100
  Profile = -> Sketch2445
  Type = 0
FEATURE [Sketcher::SketchObject] Sketch2439
  MapMode = 5
  Placement = pos=(0,0,0) rot=(1,0,0;3.14159rad)
  Support = -> [Pad1086]
  sketch-geometry (7):
    g0: LineSegment StartX=1.275 StartY=0.736122 StartZ=0 EndX=0 EndY=1.47224 EndZ=0
    g1: LineSegment StartX=0 StartY=1.47224 StartZ=0 EndX=-1.275 EndY=0.736122 EndZ=0
    g2: LineSegment StartX=-1.275 StartY=0.736122 StartZ=0 EndX=-1.275 EndY=-0.736122 EndZ=0
    g3: LineSegment StartX=-1.275 StartY=-0.736122 StartZ=0 EndX=1.34766e-11 EndY=-1.47224 EndZ=0
    g4: LineSegment StartX=1.34766e-11 StartY=-1.47224 StartZ=0 EndX=1.275 EndY=-0.736122 EndZ=0
    g5: LineSegment StartX=1.275 StartY=-0.736122 StartZ=0 EndX=1.275 EndY=0.736122 EndZ=0
    g6: Circle [constr] CenterX=0 CenterY=0 CenterZ=0 NormalX=0 NormalY=0 NormalZ=1 AngleXU=0 Radius=1.47224
  constraints (16):
    c: Coincident(g0,g1)
    c: Coincident(g1,g2)
    c: Coincident(g2,g3)
    c: Coincident(g3,g4)
    c: Coincident(g4,g5)
    c: Coincident(g5,g0)
    c: Equal(g0, g1-g5) x5
    c: PointOnObject(g0,g6)
    c: PointOnObject(g1,g6)
    c: PointOnObject(g2,g6)
    c: PointOnObject(g3,g6)
    c: PointOnObject(g4,g6)
    c: PointOnObject(g5,g6)
    c: Coincident(g6,g-1)
    c: PointOnObject(g0,g-2)
    c: DistanceX(g1,g0) = 2.55
FEATURE [PartDesign::Pocket] Pocket861  label="M3x8 Wrench167"
  BaseFeature = -> Pad1086
  Length = 1.3
  Length2 = 100
  Profile = -> Sketch2439
  Type = 0
FEATURE [PartDesign::Chamfer] Chamfer545  label="M3x8 Smooth169"
  Base = -> Pocket861 [Face11,Edge2,Edge24,Edge3]
  BaseFeature = -> Pocket861
  Size = 0.2
FEATURE [PartDesign::Body] Body706  label="M3x142"
  Group = -> [Sketch2448,Pad1082,Sketch2445,Pad1086,Sketch2439,Pocket861,Chamfer545]
  Origin = -> Origin1008
  Placement = pos=(-1.3e-14,-10,58) rot=(0,-1,0;1.5708rad)
  Tip = -> Chamfer545
FEATURE [Sketcher::SketchObject] Sketch2449
  MapMode = 5
  Placement = pos=(0,0,3) rot=(0,0,1;0rad)
  Support = -> [Pad1085]
  sketch-geometry (1):
    g0: Circle CenterX=0 CenterY=0 CenterZ=0 NormalX=0 NormalY=0 NormalZ=1 AngleXU=0 Radius=1.5
  constraints (2):
    c: Coincident(g0,g-1)
    c: Radius(g0) = 1.5
FEATURE [PartDesign::Pad] Pad1081  label="M3x8 Thread167"
  BaseFeature = -> Pad1085
  Length = 8
  Length2 = 100
  Profile = -> Sketch2449
  Type = 0
FEATURE [Sketcher::SketchObject] Sketch2446
  MapMode = 5
  Placement = pos=(0,0,0) rot=(1,0,0;3.14159rad)
  Support = -> [Pad1081]
  sketch-geometry (7):
    g0: LineSegment StartX=1.275 StartY=0.736122 StartZ=0 EndX=0 EndY=1.47224 EndZ=0
    g1: LineSegment StartX=0 StartY=1.47224 StartZ=0 EndX=-1.275 EndY=0.736122 EndZ=0
    g2: LineSegment StartX=-1.275 StartY=0.736122 StartZ=0 EndX=-1.275 EndY=-0.736122 EndZ=0
    g3: LineSegment StartX=-1.275 StartY=-0.736122 StartZ=0 EndX=1.34766e-11 EndY=-1.47224 EndZ=0
    g4: LineSegment StartX=1.34766e-11 StartY=-1.47224 StartZ=0 EndX=1.275 EndY=-0.736122 EndZ=0
    g5: LineSegment StartX=1.275 StartY=-0.736122 StartZ=0 EndX=1.275 EndY=0.736122 EndZ=0
    g6: Circle [constr] CenterX=0 CenterY=0 CenterZ=0 NormalX=0 NormalY=0 NormalZ=1 AngleXU=0 Radius=1.47224
  constraints (16):
    c: Coincident(g0,g1)
    c: Coincident(g1,g2)
    c: Coincident(g2,g3)
    c: Coincident(g3,g4)
    c: Coincident(g4,g5)
    c: Coincident(g5,g0)
    c: Equal(g0, g1-g5) x5
    c: PointOnObject(g0,g6)
    c: PointOnObject(g1,g6)
    c: PointOnObject(g2,g6)
    c: PointOnObject(g3,g6)
    c: PointOnObject(g4,g6)
    c: PointOnObject(g5,g6)
    c: Coincident(g6,g-1)
    c: PointOnObject(g0,g-2)
    c: DistanceX(g1,g0) = 2.55
FEATURE [PartDesign::Pocket] Pocket862  label="M3x8 Wrench168"
  BaseFeature = -> Pad1081
  Length = 1.3
  Length2 = 100
  Profile = -> Sketch2446
  Type = 0
FEATURE [PartDesign::Chamfer] Chamfer542  label="M3x8 Smooth166"
  Base = -> Pocket862 [Face11,Edge2,Edge24,Edge3]
  BaseFeature = -> Pocket862
  Size = 0.2
FEATURE [PartDesign::Body] Body704  label="M3x140"
  Group = -> [Sketch2447,Pad1085,Sketch2449,Pad1081,Sketch2446,Pocket862,Chamfer542]
  Origin = -> Origin1004
  Placement = pos=(-1.3e-14,20,58.05) rot=(0,-1,0;1.5708rad)
  Tip = -> Chamfer542
FEATURE [App::Part] Part277  label="Rear Shoulder Screws"
  Group = -> [Body703,Body705,Body706,Body704]
  Origin = -> Origin1007
  Placement = pos=(-240.35,-94.9,172.35) rot=(0,0,1;3.14159rad)
FEATURE [App::Part] Part269  label="Rear Legs and Shoulder"
  Group = -> [Part072,Part173,Part251,Part271,Part270,Part277,Part275]
  Origin = -> Origin972
  Placement = pos=(0.25,-0.25,-0.25) rot=(0,0,1;0rad)
FEATURE [Sketcher::SketchObject] Sketch206
  MapMode = 5
  Placement = pos=(0,0,0) rot=(1,0,0;1.5708rad)
  Support = -> [XZ_Plane1040]
  sketch-geometry (4):
    g0: LineSegment StartX=-0.32 StartY=-3 StartZ=0 EndX=0.32 EndY=-3 EndZ=0
    g1: LineSegment StartX=0.32 StartY=-3 StartZ=0 EndX=0.32 EndY=8.54 EndZ=0
    g2: LineSegment StartX=0.32 StartY=8.54 StartZ=0 EndX=-0.32 EndY=8.54 EndZ=0
    g3: LineSegment StartX=-0.32 StartY=8.54 StartZ=0 EndX=-0.32 EndY=-3 EndZ=0
  constraints (11):
    c: Coincident(g0,g1)
    c: Coincident(g1,g2)
    c: Coincident(g2,g3)
    c: Coincident(g3,g0)
    c: Horizontal(g0)
    c: Vertical(g1)
    c: Vertical(g3)
    c: DistanceY(g-1,g1) = 8.54
    c: DistanceY(g0,g-1) = 3
    c: Symmetric(g2,g1,g-2)
    c: DistanceX(g2,g2) = 0.64
FEATURE [Sketcher::SketchObject] Sketch205
  MapMode = 5
  Support = -> [XY_Plane1041]
  sketch-geometry (4):
    g0: LineSegment StartX=-1.27 StartY=-1.27 StartZ=0 EndX=1.27 EndY=-1.27 EndZ=0
    g1: LineSegment StartX=1.27 StartY=-1.27 StartZ=0 EndX=1.27 EndY=1.27 EndZ=0
    g2: LineSegment StartX=1.27 StartY=1.27 StartZ=0 EndX=-1.27 EndY=1.27 EndZ=0
    g3: LineSegment StartX=-1.27 StartY=1.27 StartZ=0 EndX=-1.27 EndY=-1.27 EndZ=0
  constraints (10):
    c: Coincident(g0,g1)
    c: Coincident(g1,g2)
    c: Coincident(g2,g3)
    c: Coincident(g3,g0)
    c: Horizontal(g0)
    c: Vertical(g3)
    c: Symmetric(g1,g2,g-2)
    c: Symmetric(g0,g1,g-1)
    c: Equal(g3,g2)
    c: DistanceX(g2,g2) = 2.54
FEATURE [Sketcher::SketchObject] Sketch204
  MapMode = 5
  Support = -> [XY_Plane1037]
  sketch-geometry (8):
    g0: LineSegment StartX=119.99 StartY=55.8663 StartZ=0 EndX=155.99 EndY=55.8663 EndZ=0
    g1: LineSegment StartX=155.99 StartY=55.8663 StartZ=0 EndX=155.99 EndY=17.7224 EndZ=0
    g2: LineSegment StartX=155.99 StartY=17.7224 StartZ=0 EndX=119.99 EndY=17.7224 EndZ=0
    g3: LineSegment StartX=119.99 StartY=17.7224 StartZ=0 EndX=119.99 EndY=55.8663 EndZ=0
    g4: Circle CenterX=124.24 CenterY=51.4724 CenterZ=0 NormalX=0 NormalY=0 NormalZ=1 AngleXU=0 Radius=1.5
    g5: Circle CenterX=152.74 CenterY=51.4724 CenterZ=0 NormalX=0 NormalY=0 NormalZ=1 AngleXU=0 Radius=1.5
    g6: Circle CenterX=152.74 CenterY=21.9724 CenterZ=0 NormalX=0 NormalY=0 NormalZ=1 AngleXU=0 Radius=1.5
    g7: Circle CenterX=124.24 CenterY=21.9724 CenterZ=0 NormalX=0 NormalY=0 NormalZ=1 AngleXU=0 Radius=1.5
  constraints (21):
    c: Coincident(g0,g1)
    c: Coincident(g1,g2)
    c: Coincident(g2,g3)
    c: Coincident(g3,g0)
    c: Horizontal(g0)
    c: Horizontal(g2)
    c: Vertical(g1)
    c: Vertical(g3)
    c: DistanceX(g0,g0) = 36
    c: Equal(g7,g4)
    c: Equal(g4,g5)
    c: Equal(g5,g6)
    c: Radius(g4) = 1.5
    c: Vertical(g7,g4)
    c: Vertical(g6,g5)
    c: Horizontal(g4,g5)
    c: Horizontal(g7,g6)
    c: DistanceX(g4,g5) = 28.5
    c: DistanceY(g7,g4) = 29.5
    c: DistanceY(g2,g7) = 4.25
    c: DistanceX(g2,g7) = 4.25
FEATURE [Sketcher::SketchObject] Sketch212
  MapMode = 5
  Support = -> [XY_Plane1017]
  sketch-geometry (8):
    g0: LineSegment StartX=120.893 StartY=55.2629 StartZ=0 EndX=155.893 EndY=55.2629 EndZ=0
    g1: LineSegment StartX=155.893 StartY=55.2629 StartZ=0 EndX=155.893 EndY=20.2629 EndZ=0
    g2: LineSegment StartX=155.893 StartY=20.2629 StartZ=0 EndX=120.893 EndY=20.2629 EndZ=0
    g3: LineSegment StartX=120.893 StartY=20.2629 StartZ=0 EndX=120.893 EndY=55.2629 EndZ=0
    g4: Circle CenterX=124.643 CenterY=51.5129 CenterZ=0 NormalX=0 NormalY=0 NormalZ=1 AngleXU=0 Radius=1.5
    g5: Circle CenterX=152.143 CenterY=51.5129 CenterZ=0 NormalX=0 NormalY=0 NormalZ=1 AngleXU=0 Radius=1.5
    g6: Circle CenterX=152.143 CenterY=24.0129 CenterZ=0 NormalX=0 NormalY=0 NormalZ=1 AngleXU=0 Radius=1.5
    g7: Circle CenterX=124.643 CenterY=24.0129 CenterZ=0 NormalX=0 NormalY=0 NormalZ=1 AngleXU=0 Radius=1.5
  constraints (22):
    c: Coincident(g0,g1)
    c: Coincident(g1,g2)
    c: Coincident(g2,g3)
    c: Coincident(g3,g0)
    c: Horizontal(g0)
    c: Horizontal(g2)
    c: Vertical(g1)
    c: Vertical(g3)
    c: DistanceX(g0,g0) = 35
    c: Equal(g3,g0)
    c: Equal(g7,g4)
    c: Equal(g4,g5)
    c: Equal(g5,g6)
    c: Radius(g4) = 1.5
    c: Vertical(g7,g4)
    c: Vertical(g6,g5)
    c: Horizontal(g4,g5)
    c: Horizontal(g7,g6)
    c: DistanceX(g4,g5) = 27.5
    c: DistanceY(g7,g4) = 27.5
    c: DistanceY(g2,g7) = 3.75
    c: DistanceX(g2,g7) = 3.75
FEATURE [Sketcher::SketchObject] Sketch2450
  MapMode = 5
  Support = -> [XY_Plane1045]
  sketch-geometry (4):
    g0: ArcOfCircle CenterX=-4 CenterY=7.5 CenterZ=0 NormalX=0 NormalY=0 NormalZ=1 AngleXU=0 Radius=1.5 StartAngle=1.5708 EndAngle=4.71239
    g1: ArcOfCircle CenterX=4 CenterY=7.5 CenterZ=0 NormalX=0 NormalY=0 NormalZ=1 AngleXU=0 Radius=1.5 StartAngle=4.71239 EndAngle=7.85398
    g2: LineSegment StartX=-4 StartY=6 StartZ=0 EndX=4 EndY=6 EndZ=0
    g3: LineSegment StartX=-4 StartY=9 StartZ=0 EndX=4 EndY=9 EndZ=0
  constraints (9):
    c: Tangent(g0,g3) = 1.5708
    c: Tangent(g0,g2) = -1.5708
    c: Tangent(g2,g1) = -1.5708
    c: Tangent(g3,g1) = 1.5708
    c: Horizontal(g2)
    c: Symmetric(g0,g1,g-2)
    c: DistanceX(g0,g1) = 8
    c: Radius(g1) = 1.5
    c: DistanceY(g-1,g0) = 7.5
FEATURE [Sketcher::SketchObject] Sketch2451
  MapMode = 5
  Support = -> [XY_Plane1044]
  sketch-geometry (4):
    g0: LineSegment StartX=-22.5 StartY=10 StartZ=0 EndX=22.5 EndY=10 EndZ=0
    g1: LineSegment StartX=22.5 StartY=10 StartZ=0 EndX=22.5 EndY=-10 EndZ=0
    g2: LineSegment StartX=22.5 StartY=-10 StartZ=0 EndX=-22.5 EndY=-10 EndZ=0
    g3: LineSegment StartX=-22.5 StartY=-10 StartZ=0 EndX=-22.5 EndY=10 EndZ=0
  constraints (10):
    c: Coincident(g0,g1)
    c: Coincident(g1,g2)
    c: Coincident(g2,g3)
    c: Coincident(g3,g0)
    c: Horizontal(g2)
    c: Vertical(g1)
    c: Symmetric(g0,g0,g-2)
    c: Symmetric(g2,g0,g-1)
    c: DistanceY(g3,g3) = 20
    c: DistanceX(g0,g0) = 45
FEATURE [Sketcher::SketchObject] Sketch216
  MapMode = 5
  Placement = pos=(0,0,0) rot=(1,0,0;1.5708rad)
  Support = -> [XZ_Plane1032]
  sketch-geometry (33):
    g0: LineSegment StartX=-1.47 StartY=-5 StartZ=0 EndX=-1.47 EndY=-4.4 EndZ=0
    g1: LineSegment StartX=-1.47 StartY=-4.4 StartZ=0 EndX=-1.57 EndY=-4.4 EndZ=0
    g2: LineSegment StartX=-1.57 StartY=-4.4 StartZ=0 EndX=-1.57 EndY=-3.4 EndZ=0
    g3: LineSegment StartX=-1.57 StartY=-3.4 StartZ=0 EndX=-1.47 EndY=-3.4 EndZ=0
    g4: LineSegment StartX=-1.47 StartY=-3.4 StartZ=0 EndX=-1.47 EndY=4.5 EndZ=0
    g5: LineSegment StartX=-1.47 StartY=4.5 StartZ=0 EndX=-1.07 EndY=4.5 EndZ=0
    g6: LineSegment StartX=-1.07 StartY=4.4 StartZ=0 EndX=-1.07 EndY=4.1 EndZ=0
    g7: LineSegment StartX=-1.07 StartY=4.1 StartZ=0 EndX=0 EndY=2.5 EndZ=0
    g8: LineSegment StartX=0 StartY=2.5 StartZ=0 EndX=-1.07 EndY=2.5 EndZ=0
    g9: LineSegment StartX=-1.07 StartY=2.5 StartZ=0 EndX=-1.07 EndY=-3.4 EndZ=0
    g10: LineSegment StartX=-1.07 StartY=-3.4 StartZ=0 EndX=-0.97 EndY=-3.4 EndZ=0
    g11: LineSegment StartX=-0.97 StartY=-3.4 StartZ=0 EndX=-0.97 EndY=-4.4 EndZ=0
    g12: LineSegment StartX=-0.97 StartY=-4.4 StartZ=0 EndX=-1.07 EndY=-4.4 EndZ=0
    g13: LineSegment StartX=-1.07 StartY=-4.4 StartZ=0 EndX=-1.07 EndY=-5 EndZ=0
    g14: LineSegment StartX=-1.07 StartY=-5 StartZ=0 EndX=-1.47 EndY=-5 EndZ=0
    g15: LineSegment StartX=1.07 StartY=-5 StartZ=0 EndX=1.47 EndY=-5 EndZ=0
    g16: LineSegment StartX=1.47 StartY=-5 StartZ=0 EndX=1.47 EndY=-4.4 EndZ=0
    g17: LineSegment StartX=1.47 StartY=-4.4 StartZ=0 EndX=1.57 EndY=-4.4 EndZ=0
    g18: LineSegment StartX=1.57 StartY=-4.4 StartZ=0 EndX=1.57 EndY=-3.4 EndZ=0
    g19: LineSegment StartX=1.57 StartY=-3.4 StartZ=0 EndX=1.47 EndY=-3.4 EndZ=0
    g20: LineSegment StartX=1.47 StartY=-3.4 StartZ=0 EndX=1.47 EndY=4.1 EndZ=0
    g21: LineSegment StartX=1.47 StartY=4.1 StartZ=0 EndX=1.2025 EndY=4.5 EndZ=0
    g22: LineSegment StartX=1.2025 StartY=4.5 StartZ=0 EndX=-0.67 EndY=4.5 EndZ=0
    g23: LineSegment StartX=-0.67 StartY=4.4 StartZ=0 EndX=-0.67 EndY=4.1 EndZ=0
    g24: LineSegment StartX=-0.67 StartY=4.1 StartZ=0 EndX=0.4 EndY=2.5 EndZ=0
    g25: LineSegment StartX=0.4 StartY=2.5 StartZ=0 EndX=1.07 EndY=2.5 EndZ=0
    g26: LineSegment StartX=1.07 StartY=2.5 StartZ=0 EndX=1.07 EndY=-3.4 EndZ=0
    g27: LineSegment StartX=1.07 StartY=-3.4 StartZ=0 EndX=0.97 EndY=-3.4 EndZ=0
    g28: LineSegment StartX=0.97 StartY=-3.4 StartZ=0 EndX=0.97 EndY=-4.4 EndZ=0
    g29: LineSegment StartX=0.97 StartY=-4.4 StartZ=0 EndX=1.07 EndY=-4.4 EndZ=0
    g30: LineSegment StartX=1.07 StartY=-4.4 StartZ=0 EndX=1.07 EndY=-5 EndZ=0
    g31: LineSegment StartX=-1.07 StartY=4.5 StartZ=0 EndX=-0.67 EndY=4.5 EndZ=0
    g32: LineSegment StartX=-1.07 StartY=4.4 StartZ=0 EndX=-0.67 EndY=4.4 EndZ=0
  constraints (97):
    c: Vertical(g0)
    c: Coincident(g0,g1)
    c: Horizontal(g1)
    c: Coincident(g1,g2)
    c: Vertical(g2)
    c: Coincident(g2,g3)
    c: Horizontal(g3)
    c: Coincident(g3,g4)
    c: Vertical(g4)
    c: Coincident(g4,g5)
    c: Horizontal(g5)
    c: Vertical(g6)
    c: Coincident(g6,g7)
    c: Coincident(g7,g8)
    c: Horizontal(g8)
    c: Coincident(g8,g9)
    c: Vertical(g9)
    c: Coincident(g9,g10)
    c: Coincident(g10,g11)
    c: Vertical(g11)
    c: Coincident(g11,g12)
    c: Coincident(g12,g13)
    c: Vertical(g13)
    c: Coincident(g13,g14)
    c: Coincident(g14,g0)
    c: Horizontal(g14)
    c: Coincident(g15,g16)
    c: Vertical(g16)
    c: Coincident(g16,g17)
    c: Horizontal(g17)
    c: Coincident(g17,g18)
    c: Vertical(g18)
    c: Coincident(g18,g19)
    c: Horizontal(g19)
    c: Coincident(g19,g20)
    c: Vertical(g20)
    c: Coincident(g20,g21)
    c: Coincident(g21,g22)
    c: Horizontal(g22)
    c: Coincident(g23,g24)
    c: Coincident(g24,g25)
    c: Horizontal(g25)
    c: Coincident(g25,g26)
    c: Vertical(g26)
    c: Coincident(g26,g27)
    c: Horizontal(g27)
    c: Coincident(g27,g28)
    c: Vertical(g28)
    c: Coincident(g28,g29)
    c: Horizontal(g29)
    c: Coincident(g29,g30)
    c: Coincident(g30,g15)
    c: Vertical(g30)
    c: Horizontal(g15)
    c: Horizontal(g5,g22)
    c: Horizontal(g7,g24)
    c: Horizontal(g6,g23)
    c: Parallel(g7,g24)
    c: Equal(g14,g15)
    c: Equal(g18,g2)
    c: Equal(g2,g11)
    c: Equal(g11,g28)
    c: Horizontal(g3,g9)
    c: Horizontal(g9,g26)
    c: Horizontal(g26,g19)
    c: Horizontal(g12)
    c: Vertical(g3,g0)
    c: Vertical(g12,g9)
    c: Vertical(g29,g26)
    c: Vertical(g19,g16)
    c: DistanceX(g0,g15) = 2.54
    c: DistanceX(g28,g17) = 0.6
    c: DistanceX(g1,g11) = 0.6
    c: DistanceX(g15,g15) = 0.4
    c: Symmetric(g13,g15,g-2)
    c: Symmetric(g11,g28,g-2)
    c: Equal(g1,g12)
    c: DistanceY(g11,g11) = 1
    c: DistanceY(g10,g-1) = 3.4
    c: DistanceY(g13,g-1) = 5
    c: Coincident(g31,g5)
    c: Coincident(g31,g22)
    c: Equal(g31,g14)
    c: Equal(g5,g31)
    c: Vertical(g23)
    c: Horizontal(g23,g20)
    c: DistanceY(g8,g4) = 2
    c: Parallel(g21,g24)
    c: PointOnObject(g7,g-2)
    c: DistanceY(g-1,g7) = 2.5
    c: Horizontal(g32)
    c: Coincident(g6,g32)
    c: Coincident(g23,g32)
    c: DistanceY(g6,g5) = 0.4
    c: Vertical(g6,g5)
    c: Vertical(g23,g22)
    c: DistanceY(g6,g5) = 0.1
FEATURE [Sketcher::SketchObject] Sketch218
  MapMode = 5
  Support = -> [XY_Plane1029]
  sketch-geometry (4):
    g0: LineSegment StartX=2.5 StartY=4 StartZ=0 EndX=4.5 EndY=4 EndZ=0
    g1: LineSegment StartX=4.5 StartY=4 StartZ=0 EndX=4.5 EndY=-4 EndZ=0
    g2: LineSegment StartX=4.5 StartY=-4 StartZ=0 EndX=2.5 EndY=-4 EndZ=0
    g3: LineSegment StartX=2.5 StartY=-4 StartZ=0 EndX=2.5 EndY=4 EndZ=0
  constraints (11):
    c: Coincident(g0,g1)
    c: Coincident(g1,g2)
    c: Coincident(g2,g3)
    c: Coincident(g3,g0)
    c: Horizontal(g0)
    c: Horizontal(g2)
    c: Vertical(g1)
    c: DistanceX(g-1,g0) = 2.5
    c: Symmetric(g0,g2,g-1)
    c: DistanceY(g3,g3) = 8
    c: DistanceX(g0,g0) = 2
FEATURE [Sketcher::SketchObject] Sketch215
  MapMode = 5
  Placement = pos=(0,0,0) rot=(1,0,0;1.5708rad)
  Support = -> [XZ_Plane1029]
  sketch-geometry (33):
    g0: LineSegment StartX=-1.47 StartY=-5 StartZ=0 EndX=-1.47 EndY=-4.4 EndZ=0
    g1: LineSegment StartX=-1.47 StartY=-4.4 StartZ=0 EndX=-1.57 EndY=-4.4 EndZ=0
    g2: LineSegment StartX=-1.57 StartY=-4.4 StartZ=0 EndX=-1.57 EndY=-3.4 EndZ=0
    g3: LineSegment StartX=-1.57 StartY=-3.4 StartZ=0 EndX=-1.47 EndY=-3.4 EndZ=0
    g4: LineSegment StartX=-1.47 StartY=-3.4 StartZ=0 EndX=-1.47 EndY=4.5 EndZ=0
    g5: LineSegment StartX=-1.47 StartY=4.5 StartZ=0 EndX=-1.07 EndY=4.5 EndZ=0
    g6: LineSegment StartX=-1.07 StartY=4.4 StartZ=0 EndX=-1.07 EndY=4.1 EndZ=0
    g7: LineSegment StartX=-1.07 StartY=4.1 StartZ=0 EndX=0 EndY=2.5 EndZ=0
    g8: LineSegment StartX=0 StartY=2.5 StartZ=0 EndX=-1.07 EndY=2.5 EndZ=0
    g9: LineSegment StartX=-1.07 StartY=2.5 StartZ=0 EndX=-1.07 EndY=-3.4 EndZ=0
    g10: LineSegment StartX=-1.07 StartY=-3.4 StartZ=0 EndX=-0.97 EndY=-3.4 EndZ=0
    g11: LineSegment StartX=-0.97 StartY=-3.4 StartZ=0 EndX=-0.97 EndY=-4.4 EndZ=0
    g12: LineSegment StartX=-0.97 StartY=-4.4 StartZ=0 EndX=-1.07 EndY=-4.4 EndZ=0
    g13: LineSegment StartX=-1.07 StartY=-4.4 StartZ=0 EndX=-1.07 EndY=-5 EndZ=0
    g14: LineSegment StartX=-1.07 StartY=-5 StartZ=0 EndX=-1.47 EndY=-5 EndZ=0
    g15: LineSegment StartX=1.07 StartY=-5 StartZ=0 EndX=1.47 EndY=-5 EndZ=0
    g16: LineSegment StartX=1.47 StartY=-5 StartZ=0 EndX=1.47 EndY=-4.4 EndZ=0
    g17: LineSegment StartX=1.47 StartY=-4.4 StartZ=0 EndX=1.57 EndY=-4.4 EndZ=0
    g18: LineSegment StartX=1.57 StartY=-4.4 StartZ=0 EndX=1.57 EndY=-3.4 EndZ=0
    g19: LineSegment StartX=1.57 StartY=-3.4 StartZ=0 EndX=1.47 EndY=-3.4 EndZ=0
    g20: LineSegment StartX=1.47 StartY=-3.4 StartZ=0 EndX=1.47 EndY=4.1 EndZ=0
    g21: LineSegment StartX=1.47 StartY=4.1 StartZ=0 EndX=1.2025 EndY=4.5 EndZ=0
    g22: LineSegment StartX=1.2025 StartY=4.5 StartZ=0 EndX=-0.67 EndY=4.5 EndZ=0
    g23: LineSegment StartX=-0.67 StartY=4.4 StartZ=0 EndX=-0.67 EndY=4.1 EndZ=0
    g24: LineSegment StartX=-0.67 StartY=4.1 StartZ=0 EndX=0.4 EndY=2.5 EndZ=0
    g25: LineSegment StartX=0.4 StartY=2.5 StartZ=0 EndX=1.07 EndY=2.5 EndZ=0
    g26: LineSegment StartX=1.07 StartY=2.5 StartZ=0 EndX=1.07 EndY=-3.4 EndZ=0
    g27: LineSegment StartX=1.07 StartY=-3.4 StartZ=0 EndX=0.97 EndY=-3.4 EndZ=0
    g28: LineSegment StartX=0.97 StartY=-3.4 StartZ=0 EndX=0.97 EndY=-4.4 EndZ=0
    g29: LineSegment StartX=0.97 StartY=-4.4 StartZ=0 EndX=1.07 EndY=-4.4 EndZ=0
    g30: LineSegment StartX=1.07 StartY=-4.4 StartZ=0 EndX=1.07 EndY=-5 EndZ=0
    g31: LineSegment StartX=-1.07 StartY=4.5 StartZ=0 EndX=-0.67 EndY=4.5 EndZ=0
    g32: LineSegment StartX=-1.07 StartY=4.4 StartZ=0 EndX=-0.67 EndY=4.4 EndZ=0
  constraints (97):
    c: Vertical(g0)
    c: Coincident(g0,g1)
    c: Horizontal(g1)
    c: Coincident(g1,g2)
    c: Vertical(g2)
    c: Coincident(g2,g3)
    c: Horizontal(g3)
    c: Coincident(g3,g4)
    c: Vertical(g4)
    c: Coincident(g4,g5)
    c: Horizontal(g5)
    c: Vertical(g6)
    c: Coincident(g6,g7)
    c: Coincident(g7,g8)
    c: Horizontal(g8)
    c: Coincident(g8,g9)
    c: Vertical(g9)
    c: Coincident(g9,g10)
    c: Coincident(g10,g11)
    c: Vertical(g11)
    c: Coincident(g11,g12)
    c: Coincident(g12,g13)
    c: Vertical(g13)
    c: Coincident(g13,g14)
    c: Coincident(g14,g0)
    c: Horizontal(g14)
    c: Coincident(g15,g16)
    c: Vertical(g16)
    c: Coincident(g16,g17)
    c: Horizontal(g17)
    c: Coincident(g17,g18)
    c: Vertical(g18)
    c: Coincident(g18,g19)
    c: Horizontal(g19)
    c: Coincident(g19,g20)
    c: Vertical(g20)
    c: Coincident(g20,g21)
    c: Coincident(g21,g22)
    c: Horizontal(g22)
    c: Coincident(g23,g24)
    c: Coincident(g24,g25)
    c: Horizontal(g25)
    c: Coincident(g25,g26)
    c: Vertical(g26)
    c: Coincident(g26,g27)
    c: Horizontal(g27)
    c: Coincident(g27,g28)
    c: Vertical(g28)
    c: Coincident(g28,g29)
    c: Horizontal(g29)
    c: Coincident(g29,g30)
    c: Coincident(g30,g15)
    c: Vertical(g30)
    c: Horizontal(g15)
    c: Horizontal(g5,g22)
    c: Horizontal(g7,g24)
    c: Horizontal(g6,g23)
    c: Parallel(g7,g24)
    c: Equal(g14,g15)
    c: Equal(g18,g2)
    c: Equal(g2,g11)
    c: Equal(g11,g28)
    c: Horizontal(g3,g9)
    c: Horizontal(g9,g26)
    c: Horizontal(g26,g19)
    c: Horizontal(g12)
    c: Vertical(g3,g0)
    c: Vertical(g12,g9)
    c: Vertical(g29,g26)
    c: Vertical(g19,g16)
    c: DistanceX(g0,g15) = 2.54
    c: DistanceX(g28,g17) = 0.6
    c: DistanceX(g1,g11) = 0.6
    c: DistanceX(g15,g15) = 0.4
    c: Symmetric(g13,g15,g-2)
    c: Symmetric(g11,g28,g-2)
    c: Equal(g1,g12)
    c: DistanceY(g11,g11) = 1
    c: DistanceY(g10,g-1) = 3.4
    c: DistanceY(g13,g-1) = 5
    c: Coincident(g31,g5)
    c: Coincident(g31,g22)
    c: Equal(g31,g14)
    c: Equal(g5,g31)
    c: Vertical(g23)
    c: Horizontal(g23,g20)
    c: DistanceY(g8,g4) = 2
    c: Parallel(g21,g24)
    c: PointOnObject(g7,g-2)
    c: DistanceY(g-1,g7) = 2.5
    c: Horizontal(g32)
    c: Coincident(g6,g32)
    c: Coincident(g23,g32)
    c: DistanceY(g6,g5) = 0.4
    c: Vertical(g6,g5)
    c: Vertical(g23,g22)
    c: DistanceY(g6,g5) = 0.1
FEATURE [Sketcher::SketchObject] Sketch203
  MapMode = 5
  Placement = pos=(0,0,0) rot=(1,0,0;1.5708rad)
  Support = -> [XZ_Plane1026]
  sketch-geometry (33):
    g0: LineSegment StartX=-1.47 StartY=-5 StartZ=0 EndX=-1.47 EndY=-4.4 EndZ=0
    g1: LineSegment StartX=-1.47 StartY=-4.4 StartZ=0 EndX=-1.57 EndY=-4.4 EndZ=0
    g2: LineSegment StartX=-1.57 StartY=-4.4 StartZ=0 EndX=-1.57 EndY=-3.4 EndZ=0
    g3: LineSegment StartX=-1.57 StartY=-3.4 StartZ=0 EndX=-1.47 EndY=-3.4 EndZ=0
    g4: LineSegment StartX=-1.47 StartY=-3.4 StartZ=0 EndX=-1.47 EndY=4.5 EndZ=0
    g5: LineSegment StartX=-1.47 StartY=4.5 StartZ=0 EndX=-1.07 EndY=4.5 EndZ=0
    g6: LineSegment StartX=-1.07 StartY=4.4 StartZ=0 EndX=-1.07 EndY=4.1 EndZ=0
    g7: LineSegment StartX=-1.07 StartY=4.1 StartZ=0 EndX=0 EndY=2.5 EndZ=0
    g8: LineSegment StartX=0 StartY=2.5 StartZ=0 EndX=-1.07 EndY=2.5 EndZ=0
    g9: LineSegment StartX=-1.07 StartY=2.5 StartZ=0 EndX=-1.07 EndY=-3.4 EndZ=0
    g10: LineSegment StartX=-1.07 StartY=-3.4 StartZ=0 EndX=-0.97 EndY=-3.4 EndZ=0
    g11: LineSegment StartX=-0.97 StartY=-3.4 StartZ=0 EndX=-0.97 EndY=-4.4 EndZ=0
    g12: LineSegment StartX=-0.97 StartY=-4.4 StartZ=0 EndX=-1.07 EndY=-4.4 EndZ=0
    g13: LineSegment StartX=-1.07 StartY=-4.4 StartZ=0 EndX=-1.07 EndY=-5 EndZ=0
    g14: LineSegment StartX=-1.07 StartY=-5 StartZ=0 EndX=-1.47 EndY=-5 EndZ=0
    g15: LineSegment StartX=1.07 StartY=-5 StartZ=0 EndX=1.47 EndY=-5 EndZ=0
    g16: LineSegment StartX=1.47 StartY=-5 StartZ=0 EndX=1.47 EndY=-4.4 EndZ=0
    g17: LineSegment StartX=1.47 StartY=-4.4 StartZ=0 EndX=1.57 EndY=-4.4 EndZ=0
    g18: LineSegment StartX=1.57 StartY=-4.4 StartZ=0 EndX=1.57 EndY=-3.4 EndZ=0
    g19: LineSegment StartX=1.57 StartY=-3.4 StartZ=0 EndX=1.47 EndY=-3.4 EndZ=0
    g20: LineSegment StartX=1.47 StartY=-3.4 StartZ=0 EndX=1.47 EndY=4.1 EndZ=0
    g21: LineSegment StartX=1.47 StartY=4.1 StartZ=0 EndX=1.2025 EndY=4.5 EndZ=0
    g22: LineSegment StartX=1.2025 StartY=4.5 StartZ=0 EndX=-0.67 EndY=4.5 EndZ=0
    g23: LineSegment StartX=-0.67 StartY=4.4 StartZ=0 EndX=-0.67 EndY=4.1 EndZ=0
    g24: LineSegment StartX=-0.67 StartY=4.1 StartZ=0 EndX=0.4 EndY=2.5 EndZ=0
    g25: LineSegment StartX=0.4 StartY=2.5 StartZ=0 EndX=1.07 EndY=2.5 EndZ=0
    g26: LineSegment StartX=1.07 StartY=2.5 StartZ=0 EndX=1.07 EndY=-3.4 EndZ=0
    g27: LineSegment StartX=1.07 StartY=-3.4 StartZ=0 EndX=0.97 EndY=-3.4 EndZ=0
    g28: LineSegment StartX=0.97 StartY=-3.4 StartZ=0 EndX=0.97 EndY=-4.4 EndZ=0
    g29: LineSegment StartX=0.97 StartY=-4.4 StartZ=0 EndX=1.07 EndY=-4.4 EndZ=0
    g30: LineSegment StartX=1.07 StartY=-4.4 StartZ=0 EndX=1.07 EndY=-5 EndZ=0
    g31: LineSegment StartX=-1.07 StartY=4.5 StartZ=0 EndX=-0.67 EndY=4.5 EndZ=0
    g32: LineSegment StartX=-1.07 StartY=4.4 StartZ=0 EndX=-0.67 EndY=4.4 EndZ=0
  constraints (97):
    c: Vertical(g0)
    c: Coincident(g0,g1)
    c: Horizontal(g1)
    c: Coincident(g1,g2)
    c: Vertical(g2)
    c: Coincident(g2,g3)
    c: Horizontal(g3)
    c: Coincident(g3,g4)
    c: Vertical(g4)
    c: Coincident(g4,g5)
    c: Horizontal(g5)
    c: Vertical(g6)
    c: Coincident(g6,g7)
    c: Coincident(g7,g8)
    c: Horizontal(g8)
    c: Coincident(g8,g9)
    c: Vertical(g9)
    c: Coincident(g9,g10)
    c: Coincident(g10,g11)
    c: Vertical(g11)
    c: Coincident(g11,g12)
    c: Coincident(g12,g13)
    c: Vertical(g13)
    c: Coincident(g13,g14)
    c: Coincident(g14,g0)
    c: Horizontal(g14)
    c: Coincident(g15,g16)
    c: Vertical(g16)
    c: Coincident(g16,g17)
    c: Horizontal(g17)
    c: Coincident(g17,g18)
    c: Vertical(g18)
    c: Coincident(g18,g19)
    c: Horizontal(g19)
    c: Coincident(g19,g20)
    c: Vertical(g20)
    c: Coincident(g20,g21)
    c: Coincident(g21,g22)
    c: Horizontal(g22)
    c: Coincident(g23,g24)
    c: Coincident(g24,g25)
    c: Horizontal(g25)
    c: Coincident(g25,g26)
    c: Vertical(g26)
    c: Coincident(g26,g27)
    c: Horizontal(g27)
    c: Coincident(g27,g28)
    c: Vertical(g28)
    c: Coincident(g28,g29)
    c: Horizontal(g29)
    c: Coincident(g29,g30)
    c: Coincident(g30,g15)
    c: Vertical(g30)
    c: Horizontal(g15)
    c: Horizontal(g5,g22)
    c: Horizontal(g7,g24)
    c: Horizontal(g6,g23)
    c: Parallel(g7,g24)
    c: Equal(g14,g15)
    c: Equal(g18,g2)
    c: Equal(g2,g11)
    c: Equal(g11,g28)
    c: Horizontal(g3,g9)
    c: Horizontal(g9,g26)
    c: Horizontal(g26,g19)
    c: Horizontal(g12)
    c: Vertical(g3,g0)
    c: Vertical(g12,g9)
    c: Vertical(g29,g26)
    c: Vertical(g19,g16)
    c: DistanceX(g0,g15) = 2.54
    c: DistanceX(g28,g17) = 0.6
    c: DistanceX(g1,g11) = 0.6
    c: DistanceX(g15,g15) = 0.4
    c: Symmetric(g13,g15,g-2)
    c: Symmetric(g11,g28,g-2)
    c: Equal(g1,g12)
    c: DistanceY(g11,g11) = 1
    c: DistanceY(g10,g-1) = 3.4
    c: DistanceY(g13,g-1) = 5
    c: Coincident(g31,g5)
    c: Coincident(g31,g22)
    c: Equal(g31,g14)
    c: Equal(g5,g31)
    c: Vertical(g23)
    c: Horizontal(g23,g20)
    c: DistanceY(g8,g4) = 2
    c: Parallel(g21,g24)
    c: PointOnObject(g7,g-2)
    c: DistanceY(g-1,g7) = 2.5
    c: Horizontal(g32)
    c: Coincident(g6,g32)
    c: Coincident(g23,g32)
    c: DistanceY(g6,g5) = 0.4
    c: Vertical(g6,g5)
    c: Vertical(g23,g22)
    c: DistanceY(g6,g5) = 0.1
FEATURE [Sketcher::SketchObject] Sketch221
  MapMode = 5
  Placement = pos=(0,0,0) rot=(1,0,0;1.5708rad)
  Support = -> [XZ_Plane056]
  sketch-geometry (6):
    g0: ArcOfCircle CenterX=8e-16 CenterY=6.1 CenterZ=0 NormalX=0 NormalY=0 NormalZ=1 AngleXU=0 Radius=2.5 StartAngle=0 EndAngle=1.5708
    g1: LineSegment StartX=2.5 StartY=6.1 StartZ=0 EndX=2.5 EndY=1 EndZ=0
    g2: LineSegment StartX=2.5 StartY=1 StartZ=0 EndX=3 EndY=1 EndZ=0
    g3: LineSegment StartX=3 StartY=1 StartZ=0 EndX=3 EndY=0 EndZ=0
    g4: LineSegment StartX=3 StartY=0 StartZ=0 EndX=0 EndY=0 EndZ=0
    g5: LineSegment StartX=-2e-16 StartY=8.6 StartZ=0 EndX=0 EndY=0 EndZ=0
  constraints (17):
    c: Coincident(g1,g0)
    c: Vertical(g1)
    c: Coincident(g2,g1)
    c: Horizontal(g2)
    c: Coincident(g3,g2)
    c: Vertical(g3)
    c: Coincident(g4,g3)
    c: Coincident(g4,g-1)
    c: Horizontal(g4)
    c: Perpendicular(g0,g-2) = 4.71239
    c: Horizontal(g0,g0)
    c: Radius(g0) = 2.5
    c: DistanceY(g4,g0) = 8.6
    c: DistanceY(g3,g3) = 1
    c: DistanceX(g4,g4) = 3
    c: Coincident(g5,g0)
    c: Coincident(g5,g4)
FEATURE [Sketcher::SketchObject] Sketch213
  MapMode = 5
  Placement = pos=(0,0,0) rot=(1,0,0;1.5708rad)
  Support = -> [XZ_Plane1032]
  sketch-geometry (6):
    g0: ArcOfCircle CenterX=8e-16 CenterY=6.1 CenterZ=0 NormalX=0 NormalY=0 NormalZ=1 AngleXU=0 Radius=2.5 StartAngle=0 EndAngle=1.5708
    g1: LineSegment StartX=2.5 StartY=6.1 StartZ=0 EndX=2.5 EndY=1 EndZ=0
    g2: LineSegment StartX=2.5 StartY=1 StartZ=0 EndX=3 EndY=1 EndZ=0
    g3: LineSegment StartX=3 StartY=1 StartZ=0 EndX=3 EndY=0 EndZ=0
    g4: LineSegment StartX=3 StartY=0 StartZ=0 EndX=0 EndY=0 EndZ=0
    g5: LineSegment StartX=-2e-16 StartY=8.6 StartZ=0 EndX=0 EndY=0 EndZ=0
  constraints (17):
    c: Coincident(g1,g0)
    c: Vertical(g1)
    c: Coincident(g2,g1)
    c: Horizontal(g2)
    c: Coincident(g3,g2)
    c: Vertical(g3)
    c: Coincident(g4,g3)
    c: Coincident(g4,g-1)
    c: Horizontal(g4)
    c: Perpendicular(g0,g-2) = 4.71239
    c: Horizontal(g0,g0)
    c: Radius(g0) = 2.5
    c: DistanceY(g4,g0) = 8.6
    c: DistanceY(g3,g3) = 1
    c: DistanceX(g4,g4) = 3
    c: Coincident(g5,g0)
    c: Coincident(g5,g4)
FEATURE [Sketcher::SketchObject] Sketch202
  MapMode = 5
  Placement = pos=(0,0,0) rot=(1,0,0;1.5708rad)
  Support = -> [XZ_Plane1027]
  sketch-geometry (33):
    g0: LineSegment StartX=-1.47 StartY=-5 StartZ=0 EndX=-1.47 EndY=-4.4 EndZ=0
    g1: LineSegment StartX=-1.47 StartY=-4.4 StartZ=0 EndX=-1.57 EndY=-4.4 EndZ=0
    g2: LineSegment StartX=-1.57 StartY=-4.4 StartZ=0 EndX=-1.57 EndY=-3.4 EndZ=0
    g3: LineSegment StartX=-1.57 StartY=-3.4 StartZ=0 EndX=-1.47 EndY=-3.4 EndZ=0
    g4: LineSegment StartX=-1.47 StartY=-3.4 StartZ=0 EndX=-1.47 EndY=4.5 EndZ=0
    g5: LineSegment StartX=-1.47 StartY=4.5 StartZ=0 EndX=-1.07 EndY=4.5 EndZ=0
    g6: LineSegment StartX=-1.07 StartY=4.4 StartZ=0 EndX=-1.07 EndY=4.1 EndZ=0
    g7: LineSegment StartX=-1.07 StartY=4.1 StartZ=0 EndX=0 EndY=2.5 EndZ=0
    g8: LineSegment StartX=0 StartY=2.5 StartZ=0 EndX=-1.07 EndY=2.5 EndZ=0
    g9: LineSegment StartX=-1.07 StartY=2.5 StartZ=0 EndX=-1.07 EndY=-3.4 EndZ=0
    g10: LineSegment StartX=-1.07 StartY=-3.4 StartZ=0 EndX=-0.97 EndY=-3.4 EndZ=0
    g11: LineSegment StartX=-0.97 StartY=-3.4 StartZ=0 EndX=-0.97 EndY=-4.4 EndZ=0
    g12: LineSegment StartX=-0.97 StartY=-4.4 StartZ=0 EndX=-1.07 EndY=-4.4 EndZ=0
    g13: LineSegment StartX=-1.07 StartY=-4.4 StartZ=0 EndX=-1.07 EndY=-5 EndZ=0
    g14: LineSegment StartX=-1.07 StartY=-5 StartZ=0 EndX=-1.47 EndY=-5 EndZ=0
    g15: LineSegment StartX=1.07 StartY=-5 StartZ=0 EndX=1.47 EndY=-5 EndZ=0
    g16: LineSegment StartX=1.47 StartY=-5 StartZ=0 EndX=1.47 EndY=-4.4 EndZ=0
    g17: LineSegment StartX=1.47 StartY=-4.4 StartZ=0 EndX=1.57 EndY=-4.4 EndZ=0
    g18: LineSegment StartX=1.57 StartY=-4.4 StartZ=0 EndX=1.57 EndY=-3.4 EndZ=0
    g19: LineSegment StartX=1.57 StartY=-3.4 StartZ=0 EndX=1.47 EndY=-3.4 EndZ=0
    g20: LineSegment StartX=1.47 StartY=-3.4 StartZ=0 EndX=1.47 EndY=4.1 EndZ=0
    g21: LineSegment StartX=1.47 StartY=4.1 StartZ=0 EndX=1.2025 EndY=4.5 EndZ=0
    g22: LineSegment StartX=1.2025 StartY=4.5 StartZ=0 EndX=-0.67 EndY=4.5 EndZ=0
    g23: LineSegment StartX=-0.67 StartY=4.4 StartZ=0 EndX=-0.67 EndY=4.1 EndZ=0
    g24: LineSegment StartX=-0.67 StartY=4.1 StartZ=0 EndX=0.4 EndY=2.5 EndZ=0
    g25: LineSegment StartX=0.4 StartY=2.5 StartZ=0 EndX=1.07 EndY=2.5 EndZ=0
    g26: LineSegment StartX=1.07 StartY=2.5 StartZ=0 EndX=1.07 EndY=-3.4 EndZ=0
    g27: LineSegment StartX=1.07 StartY=-3.4 StartZ=0 EndX=0.97 EndY=-3.4 EndZ=0
    g28: LineSegment StartX=0.97 StartY=-3.4 StartZ=0 EndX=0.97 EndY=-4.4 EndZ=0
    g29: LineSegment StartX=0.97 StartY=-4.4 StartZ=0 EndX=1.07 EndY=-4.4 EndZ=0
    g30: LineSegment StartX=1.07 StartY=-4.4 StartZ=0 EndX=1.07 EndY=-5 EndZ=0
    g31: LineSegment StartX=-1.07 StartY=4.5 StartZ=0 EndX=-0.67 EndY=4.5 EndZ=0
    g32: LineSegment StartX=-1.07 StartY=4.4 StartZ=0 EndX=-0.67 EndY=4.4 EndZ=0
  constraints (97):
    c: Vertical(g0)
    c: Coincident(g0,g1)
    c: Horizontal(g1)
    c: Coincident(g1,g2)
    c: Vertical(g2)
    c: Coincident(g2,g3)
    c: Horizontal(g3)
    c: Coincident(g3,g4)
    c: Vertical(g4)
    c: Coincident(g4,g5)
    c: Horizontal(g5)
    c: Vertical(g6)
    c: Coincident(g6,g7)
    c: Coincident(g7,g8)
    c: Horizontal(g8)
    c: Coincident(g8,g9)
    c: Vertical(g9)
    c: Coincident(g9,g10)
    c: Coincident(g10,g11)
    c: Vertical(g11)
    c: Coincident(g11,g12)
    c: Coincident(g12,g13)
    c: Vertical(g13)
    c: Coincident(g13,g14)
    c: Coincident(g14,g0)
    c: Horizontal(g14)
    c: Coincident(g15,g16)
    c: Vertical(g16)
    c: Coincident(g16,g17)
    c: Horizontal(g17)
    c: Coincident(g17,g18)
    c: Vertical(g18)
    c: Coincident(g18,g19)
    c: Horizontal(g19)
    c: Coincident(g19,g20)
    c: Vertical(g20)
    c: Coincident(g20,g21)
    c: Coincident(g21,g22)
    c: Horizontal(g22)
    c: Coincident(g23,g24)
    c: Coincident(g24,g25)
    c: Horizontal(g25)
    c: Coincident(g25,g26)
    c: Vertical(g26)
    c: Coincident(g26,g27)
    c: Horizontal(g27)
    c: Coincident(g27,g28)
    c: Vertical(g28)
    c: Coincident(g28,g29)
    c: Horizontal(g29)
    c: Coincident(g29,g30)
    c: Coincident(g30,g15)
    c: Vertical(g30)
    c: Horizontal(g15)
    c: Horizontal(g5,g22)
    c: Horizontal(g7,g24)
    c: Horizontal(g6,g23)
    c: Parallel(g7,g24)
    c: Equal(g14,g15)
    c: Equal(g18,g2)
    c: Equal(g2,g11)
    c: Equal(g11,g28)
    c: Horizontal(g3,g9)
    c: Horizontal(g9,g26)
    c: Horizontal(g26,g19)
    c: Horizontal(g12)
    c: Vertical(g3,g0)
    c: Vertical(g12,g9)
    c: Vertical(g29,g26)
    c: Vertical(g19,g16)
    c: DistanceX(g0,g15) = 2.54
    c: DistanceX(g28,g17) = 0.6
    c: DistanceX(g1,g11) = 0.6
    c: DistanceX(g15,g15) = 0.4
    c: Symmetric(g13,g15,g-2)
    c: Symmetric(g11,g28,g-2)
    c: Equal(g1,g12)
    c: DistanceY(g11,g11) = 1
    c: DistanceY(g10,g-1) = 3.4
    c: DistanceY(g13,g-1) = 5
    c: Coincident(g31,g5)
    c: Coincident(g31,g22)
    c: Equal(g31,g14)
    c: Equal(g5,g31)
    c: Vertical(g23)
    c: Horizontal(g23,g20)
    c: DistanceY(g8,g4) = 2
    c: Parallel(g21,g24)
    c: PointOnObject(g7,g-2)
    c: DistanceY(g-1,g7) = 2.5
    c: Horizontal(g32)
    c: Coincident(g6,g32)
    c: Coincident(g23,g32)
    c: DistanceY(g6,g5) = 0.4
    c: Vertical(g6,g5)
    c: Vertical(g23,g22)
    c: DistanceY(g6,g5) = 0.1
FEATURE [Sketcher::SketchObject] Sketch201
  MapMode = 5
  Support = -> [XY_Plane1027]
  sketch-geometry (4):
    g0: LineSegment StartX=2.5 StartY=4 StartZ=0 EndX=4.5 EndY=4 EndZ=0
    g1: LineSegment StartX=4.5 StartY=4 StartZ=0 EndX=4.5 EndY=-4 EndZ=0
    g2: LineSegment StartX=4.5 StartY=-4 StartZ=0 EndX=2.5 EndY=-4 EndZ=0
    g3: LineSegment StartX=2.5 StartY=-4 StartZ=0 EndX=2.5 EndY=4 EndZ=0
  constraints (11):
    c: Coincident(g0,g1)
    c: Coincident(g1,g2)
    c: Coincident(g2,g3)
    c: Coincident(g3,g0)
    c: Horizontal(g0)
    c: Horizontal(g2)
    c: Vertical(g1)
    c: DistanceX(g-1,g0) = 2.5
    c: Symmetric(g0,g2,g-1)
    c: DistanceY(g3,g3) = 8
    c: DistanceX(g0,g0) = 2
FEATURE [Sketcher::SketchObject] Sketch214
  MapMode = 5
  Support = -> [XY_Plane1033]
  sketch-geometry (4):
    g0: LineSegment StartX=2.5 StartY=4 StartZ=0 EndX=4.5 EndY=4 EndZ=0
    g1: LineSegment StartX=4.5 StartY=4 StartZ=0 EndX=4.5 EndY=-4 EndZ=0
    g2: LineSegment StartX=4.5 StartY=-4 StartZ=0 EndX=2.5 EndY=-4 EndZ=0
    g3: LineSegment StartX=2.5 StartY=-4 StartZ=0 EndX=2.5 EndY=4 EndZ=0
  constraints (11):
    c: Coincident(g0,g1)
    c: Coincident(g1,g2)
    c: Coincident(g2,g3)
    c: Coincident(g3,g0)
    c: Horizontal(g0)
    c: Horizontal(g2)
    c: Vertical(g1)
    c: DistanceX(g-1,g0) = 2.5
    c: Symmetric(g0,g2,g-1)
    c: DistanceY(g3,g3) = 8
    c: DistanceX(g0,g0) = 2
FEATURE [Sketcher::SketchObject] Sketch200
  MapMode = 5
  Placement = pos=(0,0,0) rot=(1,0,0;1.5708rad)
  Support = -> [XZ_Plane1026]
  sketch-geometry (6):
    g0: ArcOfCircle CenterX=8e-16 CenterY=6.1 CenterZ=0 NormalX=0 NormalY=0 NormalZ=1 AngleXU=0 Radius=2.5 StartAngle=0 EndAngle=1.5708
    g1: LineSegment StartX=2.5 StartY=6.1 StartZ=0 EndX=2.5 EndY=1 EndZ=0
    g2: LineSegment StartX=2.5 StartY=1 StartZ=0 EndX=3 EndY=1 EndZ=0
    g3: LineSegment StartX=3 StartY=1 StartZ=0 EndX=3 EndY=0 EndZ=0
    g4: LineSegment StartX=3 StartY=0 StartZ=0 EndX=0 EndY=0 EndZ=0
    g5: LineSegment StartX=-2e-16 StartY=8.6 StartZ=0 EndX=0 EndY=0 EndZ=0
  constraints (17):
    c: Coincident(g1,g0)
    c: Vertical(g1)
    c: Coincident(g2,g1)
    c: Horizontal(g2)
    c: Coincident(g3,g2)
    c: Vertical(g3)
    c: Coincident(g4,g3)
    c: Coincident(g4,g-1)
    c: Horizontal(g4)
    c: Perpendicular(g0,g-2) = 4.71239
    c: Horizontal(g0,g0)
    c: Radius(g0) = 2.5
    c: DistanceY(g4,g0) = 8.6
    c: DistanceY(g3,g3) = 1
    c: DistanceX(g4,g4) = 3
    c: Coincident(g5,g0)
    c: Coincident(g5,g4)
FEATURE [Sketcher::SketchObject] Sketch217
  MapMode = 5
  Placement = pos=(0,0,0) rot=(1,0,0;1.5708rad)
  Support = -> [XZ_Plane1025]
  sketch-geometry (6):
    g0: ArcOfCircle CenterX=8e-16 CenterY=6.1 CenterZ=0 NormalX=0 NormalY=0 NormalZ=1 AngleXU=0 Radius=2.5 StartAngle=0 EndAngle=1.5708
    g1: LineSegment StartX=2.5 StartY=6.1 StartZ=0 EndX=2.5 EndY=1 EndZ=0
    g2: LineSegment StartX=2.5 StartY=1 StartZ=0 EndX=3 EndY=1 EndZ=0
    g3: LineSegment StartX=3 StartY=1 StartZ=0 EndX=3 EndY=0 EndZ=0
    g4: LineSegment StartX=3 StartY=0 StartZ=0 EndX=0 EndY=0 EndZ=0
    g5: LineSegment StartX=-2e-16 StartY=8.6 StartZ=0 EndX=0 EndY=0 EndZ=0
  constraints (17):
    c: Coincident(g1,g0)
    c: Vertical(g1)
    c: Coincident(g2,g1)
    c: Horizontal(g2)
    c: Coincident(g3,g2)
    c: Vertical(g3)
    c: Coincident(g4,g3)
    c: Coincident(g4,g-1)
    c: Horizontal(g4)
    c: Perpendicular(g0,g-2) = 4.71239
    c: Horizontal(g0,g0)
    c: Radius(g0) = 2.5
    c: DistanceY(g4,g0) = 8.6
    c: DistanceY(g3,g3) = 1
    c: DistanceX(g4,g4) = 3
    c: Coincident(g5,g0)
    c: Coincident(g5,g4)
FEATURE [Sketcher::SketchObject] Sketch219
  MapMode = 5
  Placement = pos=(0,0,0) rot=(1,0,0;1.5708rad)
  Support = -> [XZ_Plane055]
  sketch-geometry (33):
    g0: LineSegment StartX=-1.47 StartY=-5 StartZ=0 EndX=-1.47 EndY=-4.4 EndZ=0
    g1: LineSegment StartX=-1.47 StartY=-4.4 StartZ=0 EndX=-1.57 EndY=-4.4 EndZ=0
    g2: LineSegment StartX=-1.57 StartY=-4.4 StartZ=0 EndX=-1.57 EndY=-3.4 EndZ=0
    g3: LineSegment StartX=-1.57 StartY=-3.4 StartZ=0 EndX=-1.47 EndY=-3.4 EndZ=0
    g4: LineSegment StartX=-1.47 StartY=-3.4 StartZ=0 EndX=-1.47 EndY=4.5 EndZ=0
    g5: LineSegment StartX=-1.47 StartY=4.5 StartZ=0 EndX=-1.07 EndY=4.5 EndZ=0
    g6: LineSegment StartX=-1.07 StartY=4.4 StartZ=0 EndX=-1.07 EndY=4.1 EndZ=0
    g7: LineSegment StartX=-1.07 StartY=4.1 StartZ=0 EndX=0 EndY=2.5 EndZ=0
    g8: LineSegment StartX=0 StartY=2.5 StartZ=0 EndX=-1.07 EndY=2.5 EndZ=0
    g9: LineSegment StartX=-1.07 StartY=2.5 StartZ=0 EndX=-1.07 EndY=-3.4 EndZ=0
    g10: LineSegment StartX=-1.07 StartY=-3.4 StartZ=0 EndX=-0.97 EndY=-3.4 EndZ=0
    g11: LineSegment StartX=-0.97 StartY=-3.4 StartZ=0 EndX=-0.97 EndY=-4.4 EndZ=0
    g12: LineSegment StartX=-0.97 StartY=-4.4 StartZ=0 EndX=-1.07 EndY=-4.4 EndZ=0
    g13: LineSegment StartX=-1.07 StartY=-4.4 StartZ=0 EndX=-1.07 EndY=-5 EndZ=0
    g14: LineSegment StartX=-1.07 StartY=-5 StartZ=0 EndX=-1.47 EndY=-5 EndZ=0
    g15: LineSegment StartX=1.07 StartY=-5 StartZ=0 EndX=1.47 EndY=-5 EndZ=0
    g16: LineSegment StartX=1.47 StartY=-5 StartZ=0 EndX=1.47 EndY=-4.4 EndZ=0
    g17: LineSegment StartX=1.47 StartY=-4.4 StartZ=0 EndX=1.57 EndY=-4.4 EndZ=0
    g18: LineSegment StartX=1.57 StartY=-4.4 StartZ=0 EndX=1.57 EndY=-3.4 EndZ=0
    g19: LineSegment StartX=1.57 StartY=-3.4 StartZ=0 EndX=1.47 EndY=-3.4 EndZ=0
    g20: LineSegment StartX=1.47 StartY=-3.4 StartZ=0 EndX=1.47 EndY=4.1 EndZ=0
    g21: LineSegment StartX=1.47 StartY=4.1 StartZ=0 EndX=1.2025 EndY=4.5 EndZ=0
    g22: LineSegment StartX=1.2025 StartY=4.5 StartZ=0 EndX=-0.67 EndY=4.5 EndZ=0
    g23: LineSegment StartX=-0.67 StartY=4.4 StartZ=0 EndX=-0.67 EndY=4.1 EndZ=0
    g24: LineSegment StartX=-0.67 StartY=4.1 StartZ=0 EndX=0.4 EndY=2.5 EndZ=0
    g25: LineSegment StartX=0.4 StartY=2.5 StartZ=0 EndX=1.07 EndY=2.5 EndZ=0
    g26: LineSegment StartX=1.07 StartY=2.5 StartZ=0 EndX=1.07 EndY=-3.4 EndZ=0
    g27: LineSegment StartX=1.07 StartY=-3.4 StartZ=0 EndX=0.97 EndY=-3.4 EndZ=0
    g28: LineSegment StartX=0.97 StartY=-3.4 StartZ=0 EndX=0.97 EndY=-4.4 EndZ=0
    g29: LineSegment StartX=0.97 StartY=-4.4 StartZ=0 EndX=1.07 EndY=-4.4 EndZ=0
    g30: LineSegment StartX=1.07 StartY=-4.4 StartZ=0 EndX=1.07 EndY=-5 EndZ=0
    g31: LineSegment StartX=-1.07 StartY=4.5 StartZ=0 EndX=-0.67 EndY=4.5 EndZ=0
    g32: LineSegment StartX=-1.07 StartY=4.4 StartZ=0 EndX=-0.67 EndY=4.4 EndZ=0
  constraints (97):
    c: Vertical(g0)
    c: Coincident(g0,g1)
    c: Horizontal(g1)
    c: Coincident(g1,g2)
    c: Vertical(g2)
    c: Coincident(g2,g3)
    c: Horizontal(g3)
    c: Coincident(g3,g4)
    c: Vertical(g4)
    c: Coincident(g4,g5)
    c: Horizontal(g5)
    c: Vertical(g6)
    c: Coincident(g6,g7)
    c: Coincident(g7,g8)
    c: Horizontal(g8)
    c: Coincident(g8,g9)
    c: Vertical(g9)
    c: Coincident(g9,g10)
    c: Coincident(g10,g11)
    c: Vertical(g11)
    c: Coincident(g11,g12)
    c: Coincident(g12,g13)
    c: Vertical(g13)
    c: Coincident(g13,g14)
    c: Coincident(g14,g0)
    c: Horizontal(g14)
    c: Coincident(g15,g16)
    c: Vertical(g16)
    c: Coincident(g16,g17)
    c: Horizontal(g17)
    c: Coincident(g17,g18)
    c: Vertical(g18)
    c: Coincident(g18,g19)
    c: Horizontal(g19)
    c: Coincident(g19,g20)
    c: Vertical(g20)
    c: Coincident(g20,g21)
    c: Coincident(g21,g22)
    c: Horizontal(g22)
    c: Coincident(g23,g24)
    c: Coincident(g24,g25)
    c: Horizontal(g25)
    c: Coincident(g25,g26)
    c: Vertical(g26)
    c: Coincident(g26,g27)
    c: Horizontal(g27)
    c: Coincident(g27,g28)
    c: Vertical(g28)
    c: Coincident(g28,g29)
    c: Horizontal(g29)
    c: Coincident(g29,g30)
    c: Coincident(g30,g15)
    c: Vertical(g30)
    c: Horizontal(g15)
    c: Horizontal(g5,g22)
    c: Horizontal(g7,g24)
    c: Horizontal(g6,g23)
    c: Parallel(g7,g24)
    c: Equal(g14,g15)
    c: Equal(g18,g2)
    c: Equal(g2,g11)
    c: Equal(g11,g28)
    c: Horizontal(g3,g9)
    c: Horizontal(g9,g26)
    c: Horizontal(g26,g19)
    c: Horizontal(g12)
    c: Vertical(g3,g0)
    c: Vertical(g12,g9)
    c: Vertical(g29,g26)
    c: Vertical(g19,g16)
    c: DistanceX(g0,g15) = 2.54
    c: DistanceX(g28,g17) = 0.6
    c: DistanceX(g1,g11) = 0.6
    c: DistanceX(g15,g15) = 0.4
    c: Symmetric(g13,g15,g-2)
    c: Symmetric(g11,g28,g-2)
    c: Equal(g1,g12)
    c: DistanceY(g11,g11) = 1
    c: DistanceY(g10,g-1) = 3.4
    c: DistanceY(g13,g-1) = 5
    c: Coincident(g31,g5)
    c: Coincident(g31,g22)
    c: Equal(g31,g14)
    c: Equal(g5,g31)
    c: Vertical(g23)
    c: Horizontal(g23,g20)
    c: DistanceY(g8,g4) = 2
    c: Parallel(g21,g24)
    c: PointOnObject(g7,g-2)
    c: DistanceY(g-1,g7) = 2.5
    c: Horizontal(g32)
    c: Coincident(g6,g32)
    c: Coincident(g23,g32)
    c: DistanceY(g6,g5) = 0.4
    c: Vertical(g6,g5)
    c: Vertical(g23,g22)
    c: DistanceY(g6,g5) = 0.1
FEATURE [Sketcher::SketchObject] Sketch220
  MapMode = 5
  Placement = pos=(0,0,0) rot=(1,0,0;1.5708rad)
  Support = -> [XZ_Plane1025]
  sketch-geometry (33):
    g0: LineSegment StartX=-1.47 StartY=-5 StartZ=0 EndX=-1.47 EndY=-4.4 EndZ=0
    g1: LineSegment StartX=-1.47 StartY=-4.4 StartZ=0 EndX=-1.57 EndY=-4.4 EndZ=0
    g2: LineSegment StartX=-1.57 StartY=-4.4 StartZ=0 EndX=-1.57 EndY=-3.4 EndZ=0
    g3: LineSegment StartX=-1.57 StartY=-3.4 StartZ=0 EndX=-1.47 EndY=-3.4 EndZ=0
    g4: LineSegment StartX=-1.47 StartY=-3.4 StartZ=0 EndX=-1.47 EndY=4.5 EndZ=0
    g5: LineSegment StartX=-1.47 StartY=4.5 StartZ=0 EndX=-1.07 EndY=4.5 EndZ=0
    g6: LineSegment StartX=-1.07 StartY=4.4 StartZ=0 EndX=-1.07 EndY=4.1 EndZ=0
    g7: LineSegment StartX=-1.07 StartY=4.1 StartZ=0 EndX=0 EndY=2.5 EndZ=0
    g8: LineSegment StartX=0 StartY=2.5 StartZ=0 EndX=-1.07 EndY=2.5 EndZ=0
    g9: LineSegment StartX=-1.07 StartY=2.5 StartZ=0 EndX=-1.07 EndY=-3.4 EndZ=0
    g10: LineSegment StartX=-1.07 StartY=-3.4 StartZ=0 EndX=-0.97 EndY=-3.4 EndZ=0
    g11: LineSegment StartX=-0.97 StartY=-3.4 StartZ=0 EndX=-0.97 EndY=-4.4 EndZ=0
    g12: LineSegment StartX=-0.97 StartY=-4.4 StartZ=0 EndX=-1.07 EndY=-4.4 EndZ=0
    g13: LineSegment StartX=-1.07 StartY=-4.4 StartZ=0 EndX=-1.07 EndY=-5 EndZ=0
    g14: LineSegment StartX=-1.07 StartY=-5 StartZ=0 EndX=-1.47 EndY=-5 EndZ=0
    g15: LineSegment StartX=1.07 StartY=-5 StartZ=0 EndX=1.47 EndY=-5 EndZ=0
    g16: LineSegment StartX=1.47 StartY=-5 StartZ=0 EndX=1.47 EndY=-4.4 EndZ=0
    g17: LineSegment StartX=1.47 StartY=-4.4 StartZ=0 EndX=1.57 EndY=-4.4 EndZ=0
    g18: LineSegment StartX=1.57 StartY=-4.4 StartZ=0 EndX=1.57 EndY=-3.4 EndZ=0
    g19: LineSegment StartX=1.57 StartY=-3.4 StartZ=0 EndX=1.47 EndY=-3.4 EndZ=0
    g20: LineSegment StartX=1.47 StartY=-3.4 StartZ=0 EndX=1.47 EndY=4.1 EndZ=0
    g21: LineSegment StartX=1.47 StartY=4.1 StartZ=0 EndX=1.2025 EndY=4.5 EndZ=0
    g22: LineSegment StartX=1.2025 StartY=4.5 StartZ=0 EndX=-0.67 EndY=4.5 EndZ=0
    g23: LineSegment StartX=-0.67 StartY=4.4 StartZ=0 EndX=-0.67 EndY=4.1 EndZ=0
    g24: LineSegment StartX=-0.67 StartY=4.1 StartZ=0 EndX=0.4 EndY=2.5 EndZ=0
    g25: LineSegment StartX=0.4 StartY=2.5 StartZ=0 EndX=1.07 EndY=2.5 EndZ=0
    g26: LineSegment StartX=1.07 StartY=2.5 StartZ=0 EndX=1.07 EndY=-3.4 EndZ=0
    g27: LineSegment StartX=1.07 StartY=-3.4 StartZ=0 EndX=0.97 EndY=-3.4 EndZ=0
    g28: LineSegment StartX=0.97 StartY=-3.4 StartZ=0 EndX=0.97 EndY=-4.4 EndZ=0
    g29: LineSegment StartX=0.97 StartY=-4.4 StartZ=0 EndX=1.07 EndY=-4.4 EndZ=0
    g30: LineSegment StartX=1.07 StartY=-4.4 StartZ=0 EndX=1.07 EndY=-5 EndZ=0
    g31: LineSegment StartX=-1.07 StartY=4.5 StartZ=0 EndX=-0.67 EndY=4.5 EndZ=0
    g32: LineSegment StartX=-1.07 StartY=4.4 StartZ=0 EndX=-0.67 EndY=4.4 EndZ=0
  constraints (97):
    c: Vertical(g0)
    c: Coincident(g0,g1)
    c: Horizontal(g1)
    c: Coincident(g1,g2)
    c: Vertical(g2)
    c: Coincident(g2,g3)
    c: Horizontal(g3)
    c: Coincident(g3,g4)
    c: Vertical(g4)
    c: Coincident(g4,g5)
    c: Horizontal(g5)
    c: Vertical(g6)
    c: Coincident(g6,g7)
    c: Coincident(g7,g8)
    c: Horizontal(g8)
    c: Coincident(g8,g9)
    c: Vertical(g9)
    c: Coincident(g9,g10)
    c: Coincident(g10,g11)
    c: Vertical(g11)
    c: Coincident(g11,g12)
    c: Coincident(g12,g13)
    c: Vertical(g13)
    c: Coincident(g13,g14)
    c: Coincident(g14,g0)
    c: Horizontal(g14)
    c: Coincident(g15,g16)
    c: Vertical(g16)
    c: Coincident(g16,g17)
    c: Horizontal(g17)
    c: Coincident(g17,g18)
    c: Vertical(g18)
    c: Coincident(g18,g19)
    c: Horizontal(g19)
    c: Coincident(g19,g20)
    c: Vertical(g20)
    c: Coincident(g20,g21)
    c: Coincident(g21,g22)
    c: Horizontal(g22)
    c: Coincident(g23,g24)
    c: Coincident(g24,g25)
    c: Horizontal(g25)
    c: Coincident(g25,g26)
    c: Vertical(g26)
    c: Coincident(g26,g27)
    c: Horizontal(g27)
    c: Coincident(g27,g28)
    c: Vertical(g28)
    c: Coincident(g28,g29)
    c: Horizontal(g29)
    c: Coincident(g29,g30)
    c: Coincident(g30,g15)
    c: Vertical(g30)
    c: Horizontal(g15)
    c: Horizontal(g5,g22)
    c: Horizontal(g7,g24)
    c: Horizontal(g6,g23)
    c: Parallel(g7,g24)
    c: Equal(g14,g15)
    c: Equal(g18,g2)
    c: Equal(g2,g11)
    c: Equal(g11,g28)
    c: Horizontal(g3,g9)
    c: Horizontal(g9,g26)
    c: Horizontal(g26,g19)
    c: Horizontal(g12)
    c: Vertical(g3,g0)
    c: Vertical(g12,g9)
    c: Vertical(g29,g26)
    c: Vertical(g19,g16)
    c: DistanceX(g0,g15) = 2.54
    c: DistanceX(g28,g17) = 0.6
    c: DistanceX(g1,g11) = 0.6
    c: DistanceX(g15,g15) = 0.4
    c: Symmetric(g13,g15,g-2)
    c: Symmetric(g11,g28,g-2)
    c: Equal(g1,g12)
    c: DistanceY(g11,g11) = 1
    c: DistanceY(g10,g-1) = 3.4
    c: DistanceY(g13,g-1) = 5
    c: Coincident(g31,g5)
    c: Coincident(g31,g22)
    c: Equal(g31,g14)
    c: Equal(g5,g31)
    c: Vertical(g23)
    c: Horizontal(g23,g20)
    c: DistanceY(g8,g4) = 2
    c: Parallel(g21,g24)
    c: PointOnObject(g7,g-2)
    c: DistanceY(g-1,g7) = 2.5
    c: Horizontal(g32)
    c: Coincident(g6,g32)
    c: Coincident(g23,g32)
    c: DistanceY(g6,g5) = 0.4
    c: Vertical(g6,g5)
    c: Vertical(g23,g22)
    c: DistanceY(g6,g5) = 0.1
FEATURE [Sketcher::SketchObject] Sketch230
  MapMode = 5
  Support = -> [XY_Plane1021]
  sketch-geometry (4):
    g0: LineSegment StartX=2.5 StartY=4 StartZ=0 EndX=4.5 EndY=4 EndZ=0
    g1: LineSegment StartX=4.5 StartY=4 StartZ=0 EndX=4.5 EndY=-4 EndZ=0
    g2: LineSegment StartX=4.5 StartY=-4 StartZ=0 EndX=2.5 EndY=-4 EndZ=0
    g3: LineSegment StartX=2.5 StartY=-4 StartZ=0 EndX=2.5 EndY=4 EndZ=0
  constraints (11):
    c: Coincident(g0,g1)
    c: Coincident(g1,g2)
    c: Coincident(g2,g3)
    c: Coincident(g3,g0)
    c: Horizontal(g0)
    c: Horizontal(g2)
    c: Vertical(g1)
    c: DistanceX(g-1,g0) = 2.5
    c: Symmetric(g0,g2,g-1)
    c: DistanceY(g3,g3) = 8
    c: DistanceX(g0,g0) = 2
FEATURE [Sketcher::SketchObject] Sketch232
  MapMode = 5
  Placement = pos=(0,0,0) rot=(1,0,0;1.5708rad)
  Support = -> [XZ_Plane1022]
  sketch-geometry (33):
    g0: LineSegment StartX=-1.47 StartY=-5 StartZ=0 EndX=-1.47 EndY=-4.4 EndZ=0
    g1: LineSegment StartX=-1.47 StartY=-4.4 StartZ=0 EndX=-1.57 EndY=-4.4 EndZ=0
    g2: LineSegment StartX=-1.57 StartY=-4.4 StartZ=0 EndX=-1.57 EndY=-3.4 EndZ=0
    g3: LineSegment StartX=-1.57 StartY=-3.4 StartZ=0 EndX=-1.47 EndY=-3.4 EndZ=0
    g4: LineSegment StartX=-1.47 StartY=-3.4 StartZ=0 EndX=-1.47 EndY=4.5 EndZ=0
    g5: LineSegment StartX=-1.47 StartY=4.5 StartZ=0 EndX=-1.07 EndY=4.5 EndZ=0
    g6: LineSegment StartX=-1.07 StartY=4.4 StartZ=0 EndX=-1.07 EndY=4.1 EndZ=0
    g7: LineSegment StartX=-1.07 StartY=4.1 StartZ=0 EndX=0 EndY=2.5 EndZ=0
    g8: LineSegment StartX=0 StartY=2.5 StartZ=0 EndX=-1.07 EndY=2.5 EndZ=0
    g9: LineSegment StartX=-1.07 StartY=2.5 StartZ=0 EndX=-1.07 EndY=-3.4 EndZ=0
    g10: LineSegment StartX=-1.07 StartY=-3.4 StartZ=0 EndX=-0.97 EndY=-3.4 EndZ=0
    g11: LineSegment StartX=-0.97 StartY=-3.4 StartZ=0 EndX=-0.97 EndY=-4.4 EndZ=0
    g12: LineSegment StartX=-0.97 StartY=-4.4 StartZ=0 EndX=-1.07 EndY=-4.4 EndZ=0
    g13: LineSegment StartX=-1.07 StartY=-4.4 StartZ=0 EndX=-1.07 EndY=-5 EndZ=0
    g14: LineSegment StartX=-1.07 StartY=-5 StartZ=0 EndX=-1.47 EndY=-5 EndZ=0
    g15: LineSegment StartX=1.07 StartY=-5 StartZ=0 EndX=1.47 EndY=-5 EndZ=0
    g16: LineSegment StartX=1.47 StartY=-5 StartZ=0 EndX=1.47 EndY=-4.4 EndZ=0
    g17: LineSegment StartX=1.47 StartY=-4.4 StartZ=0 EndX=1.57 EndY=-4.4 EndZ=0
    g18: LineSegment StartX=1.57 StartY=-4.4 StartZ=0 EndX=1.57 EndY=-3.4 EndZ=0
    g19: LineSegment StartX=1.57 StartY=-3.4 StartZ=0 EndX=1.47 EndY=-3.4 EndZ=0
    g20: LineSegment StartX=1.47 StartY=-3.4 StartZ=0 EndX=1.47 EndY=4.1 EndZ=0
    g21: LineSegment StartX=1.47 StartY=4.1 StartZ=0 EndX=1.2025 EndY=4.5 EndZ=0
    g22: LineSegment StartX=1.2025 StartY=4.5 StartZ=0 EndX=-0.67 EndY=4.5 EndZ=0
    g23: LineSegment StartX=-0.67 StartY=4.4 StartZ=0 EndX=-0.67 EndY=4.1 EndZ=0
    g24: LineSegment StartX=-0.67 StartY=4.1 StartZ=0 EndX=0.4 EndY=2.5 EndZ=0
    g25: LineSegment StartX=0.4 StartY=2.5 StartZ=0 EndX=1.07 EndY=2.5 EndZ=0
    g26: LineSegment StartX=1.07 StartY=2.5 StartZ=0 EndX=1.07 EndY=-3.4 EndZ=0
    g27: LineSegment StartX=1.07 StartY=-3.4 StartZ=0 EndX=0.97 EndY=-3.4 EndZ=0
    g28: LineSegment StartX=0.97 StartY=-3.4 StartZ=0 EndX=0.97 EndY=-4.4 EndZ=0
    g29: LineSegment StartX=0.97 StartY=-4.4 StartZ=0 EndX=1.07 EndY=-4.4 EndZ=0
    g30: LineSegment StartX=1.07 StartY=-4.4 StartZ=0 EndX=1.07 EndY=-5 EndZ=0
    g31: LineSegment StartX=-1.07 StartY=4.5 StartZ=0 EndX=-0.67 EndY=4.5 EndZ=0
    g32: LineSegment StartX=-1.07 StartY=4.4 StartZ=0 EndX=-0.67 EndY=4.4 EndZ=0
  constraints (97):
    c: Vertical(g0)
    c: Coincident(g0,g1)
    c: Horizontal(g1)
    c: Coincident(g1,g2)
    c: Vertical(g2)
    c: Coincident(g2,g3)
    c: Horizontal(g3)
    c: Coincident(g3,g4)
    c: Vertical(g4)
    c: Coincident(g4,g5)
    c: Horizontal(g5)
    c: Vertical(g6)
    c: Coincident(g6,g7)
    c: Coincident(g7,g8)
    c: Horizontal(g8)
    c: Coincident(g8,g9)
    c: Vertical(g9)
    c: Coincident(g9,g10)
    c: Coincident(g10,g11)
    c: Vertical(g11)
    c: Coincident(g11,g12)
    c: Coincident(g12,g13)
    c: Vertical(g13)
    c: Coincident(g13,g14)
    c: Coincident(g14,g0)
    c: Horizontal(g14)
    c: Coincident(g15,g16)
    c: Vertical(g16)
    c: Coincident(g16,g17)
    c: Horizontal(g17)
    c: Coincident(g17,g18)
    c: Vertical(g18)
    c: Coincident(g18,g19)
    c: Horizontal(g19)
    c: Coincident(g19,g20)
    c: Vertical(g20)
    c: Coincident(g20,g21)
    c: Coincident(g21,g22)
    c: Horizontal(g22)
    c: Coincident(g23,g24)
    c: Coincident(g24,g25)
    c: Horizontal(g25)
    c: Coincident(g25,g26)
    c: Vertical(g26)
    c: Coincident(g26,g27)
    c: Horizontal(g27)
    c: Coincident(g27,g28)
    c: Vertical(g28)
    c: Coincident(g28,g29)
    c: Horizontal(g29)
    c: Coincident(g29,g30)
    c: Coincident(g30,g15)
    c: Vertical(g30)
    c: Horizontal(g15)
    c: Horizontal(g5,g22)
    c: Horizontal(g7,g24)
    c: Horizontal(g6,g23)
    c: Parallel(g7,g24)
    c: Equal(g14,g15)
    c: Equal(g18,g2)
    c: Equal(g2,g11)
    c: Equal(g11,g28)
    c: Horizontal(g3,g9)
    c: Horizontal(g9,g26)
    c: Horizontal(g26,g19)
    c: Horizontal(g12)
    c: Vertical(g3,g0)
    c: Vertical(g12,g9)
    c: Vertical(g29,g26)
    c: Vertical(g19,g16)
    c: DistanceX(g0,g15) = 2.54
    c: DistanceX(g28,g17) = 0.6
    c: DistanceX(g1,g11) = 0.6
    c: DistanceX(g15,g15) = 0.4
    c: Symmetric(g13,g15,g-2)
    c: Symmetric(g11,g28,g-2)
    c: Equal(g1,g12)
    c: DistanceY(g11,g11) = 1
    c: DistanceY(g10,g-1) = 3.4
    c: DistanceY(g13,g-1) = 5
    c: Coincident(g31,g5)
    c: Coincident(g31,g22)
    c: Equal(g31,g14)
    c: Equal(g5,g31)
    c: Vertical(g23)
    c: Horizontal(g23,g20)
    c: DistanceY(g8,g4) = 2
    c: Parallel(g21,g24)
    c: PointOnObject(g7,g-2)
    c: DistanceY(g-1,g7) = 2.5
    c: Horizontal(g32)
    c: Coincident(g6,g32)
    c: Coincident(g23,g32)
    c: DistanceY(g6,g5) = 0.4
    c: Vertical(g6,g5)
    c: Vertical(g23,g22)
    c: DistanceY(g6,g5) = 0.1
FEATURE [Sketcher::SketchObject] Sketch227
  MapMode = 5
  Placement = pos=(0,0,0) rot=(1,0,0;1.5708rad)
  Support = -> [XZ_Plane1034]
  sketch-geometry (33):
    g0: LineSegment StartX=-1.47 StartY=-5 StartZ=0 EndX=-1.47 EndY=-4.4 EndZ=0
    g1: LineSegment StartX=-1.47 StartY=-4.4 StartZ=0 EndX=-1.57 EndY=-4.4 EndZ=0
    g2: LineSegment StartX=-1.57 StartY=-4.4 StartZ=0 EndX=-1.57 EndY=-3.4 EndZ=0
    g3: LineSegment StartX=-1.57 StartY=-3.4 StartZ=0 EndX=-1.47 EndY=-3.4 EndZ=0
    g4: LineSegment StartX=-1.47 StartY=-3.4 StartZ=0 EndX=-1.47 EndY=4.5 EndZ=0
    g5: LineSegment StartX=-1.47 StartY=4.5 StartZ=0 EndX=-1.07 EndY=4.5 EndZ=0
    g6: LineSegment StartX=-1.07 StartY=4.4 StartZ=0 EndX=-1.07 EndY=4.1 EndZ=0
    g7: LineSegment StartX=-1.07 StartY=4.1 StartZ=0 EndX=0 EndY=2.5 EndZ=0
    g8: LineSegment StartX=0 StartY=2.5 StartZ=0 EndX=-1.07 EndY=2.5 EndZ=0
    g9: LineSegment StartX=-1.07 StartY=2.5 StartZ=0 EndX=-1.07 EndY=-3.4 EndZ=0
    g10: LineSegment StartX=-1.07 StartY=-3.4 StartZ=0 EndX=-0.97 EndY=-3.4 EndZ=0
    g11: LineSegment StartX=-0.97 StartY=-3.4 StartZ=0 EndX=-0.97 EndY=-4.4 EndZ=0
    g12: LineSegment StartX=-0.97 StartY=-4.4 StartZ=0 EndX=-1.07 EndY=-4.4 EndZ=0
    g13: LineSegment StartX=-1.07 StartY=-4.4 StartZ=0 EndX=-1.07 EndY=-5 EndZ=0
    g14: LineSegment StartX=-1.07 StartY=-5 StartZ=0 EndX=-1.47 EndY=-5 EndZ=0
    g15: LineSegment StartX=1.07 StartY=-5 StartZ=0 EndX=1.47 EndY=-5 EndZ=0
    g16: LineSegment StartX=1.47 StartY=-5 StartZ=0 EndX=1.47 EndY=-4.4 EndZ=0
    g17: LineSegment StartX=1.47 StartY=-4.4 StartZ=0 EndX=1.57 EndY=-4.4 EndZ=0
    g18: LineSegment StartX=1.57 StartY=-4.4 StartZ=0 EndX=1.57 EndY=-3.4 EndZ=0
    g19: LineSegment StartX=1.57 StartY=-3.4 StartZ=0 EndX=1.47 EndY=-3.4 EndZ=0
    g20: LineSegment StartX=1.47 StartY=-3.4 StartZ=0 EndX=1.47 EndY=4.1 EndZ=0
    g21: LineSegment StartX=1.47 StartY=4.1 StartZ=0 EndX=1.2025 EndY=4.5 EndZ=0
    g22: LineSegment StartX=1.2025 StartY=4.5 StartZ=0 EndX=-0.67 EndY=4.5 EndZ=0
    g23: LineSegment StartX=-0.67 StartY=4.4 StartZ=0 EndX=-0.67 EndY=4.1 EndZ=0
    g24: LineSegment StartX=-0.67 StartY=4.1 StartZ=0 EndX=0.4 EndY=2.5 EndZ=0
    g25: LineSegment StartX=0.4 StartY=2.5 StartZ=0 EndX=1.07 EndY=2.5 EndZ=0
    g26: LineSegment StartX=1.07 StartY=2.5 StartZ=0 EndX=1.07 EndY=-3.4 EndZ=0
    g27: LineSegment StartX=1.07 StartY=-3.4 StartZ=0 EndX=0.97 EndY=-3.4 EndZ=0
    g28: LineSegment StartX=0.97 StartY=-3.4 StartZ=0 EndX=0.97 EndY=-4.4 EndZ=0
    g29: LineSegment StartX=0.97 StartY=-4.4 StartZ=0 EndX=1.07 EndY=-4.4 EndZ=0
    g30: LineSegment StartX=1.07 StartY=-4.4 StartZ=0 EndX=1.07 EndY=-5 EndZ=0
    g31: LineSegment StartX=-1.07 StartY=4.5 StartZ=0 EndX=-0.67 EndY=4.5 EndZ=0
    g32: LineSegment StartX=-1.07 StartY=4.4 StartZ=0 EndX=-0.67 EndY=4.4 EndZ=0
  constraints (97):
    c: Vertical(g0)
    c: Coincident(g0,g1)
    c: Horizontal(g1)
    c: Coincident(g1,g2)
    c: Vertical(g2)
    c: Coincident(g2,g3)
    c: Horizontal(g3)
    c: Coincident(g3,g4)
    c: Vertical(g4)
    c: Coincident(g4,g5)
    c: Horizontal(g5)
    c: Vertical(g6)
    c: Coincident(g6,g7)
    c: Coincident(g7,g8)
    c: Horizontal(g8)
    c: Coincident(g8,g9)
    c: Vertical(g9)
    c: Coincident(g9,g10)
    c: Coincident(g10,g11)
    c: Vertical(g11)
    c: Coincident(g11,g12)
    c: Coincident(g12,g13)
    c: Vertical(g13)
    c: Coincident(g13,g14)
    c: Coincident(g14,g0)
    c: Horizontal(g14)
    c: Coincident(g15,g16)
    c: Vertical(g16)
    c: Coincident(g16,g17)
    c: Horizontal(g17)
    c: Coincident(g17,g18)
    c: Vertical(g18)
    c: Coincident(g18,g19)
    c: Horizontal(g19)
    c: Coincident(g19,g20)
    c: Vertical(g20)
    c: Coincident(g20,g21)
    c: Coincident(g21,g22)
    c: Horizontal(g22)
    c: Coincident(g23,g24)
    c: Coincident(g24,g25)
    c: Horizontal(g25)
    c: Coincident(g25,g26)
    c: Vertical(g26)
    c: Coincident(g26,g27)
    c: Horizontal(g27)
    c: Coincident(g27,g28)
    c: Vertical(g28)
    c: Coincident(g28,g29)
    c: Horizontal(g29)
    c: Coincident(g29,g30)
    c: Coincident(g30,g15)
    c: Vertical(g30)
    c: Horizontal(g15)
    c: Horizontal(g5,g22)
    c: Horizontal(g7,g24)
    c: Horizontal(g6,g23)
    c: Parallel(g7,g24)
    c: Equal(g14,g15)
    c: Equal(g18,g2)
    c: Equal(g2,g11)
    c: Equal(g11,g28)
    c: Horizontal(g3,g9)
    c: Horizontal(g9,g26)
    c: Horizontal(g26,g19)
    c: Horizontal(g12)
    c: Vertical(g3,g0)
    c: Vertical(g12,g9)
    c: Vertical(g29,g26)
    c: Vertical(g19,g16)
    c: DistanceX(g0,g15) = 2.54
    c: DistanceX(g28,g17) = 0.6
    c: DistanceX(g1,g11) = 0.6
    c: DistanceX(g15,g15) = 0.4
    c: Symmetric(g13,g15,g-2)
    c: Symmetric(g11,g28,g-2)
    c: Equal(g1,g12)
    c: DistanceY(g11,g11) = 1
    c: DistanceY(g10,g-1) = 3.4
    c: DistanceY(g13,g-1) = 5
    c: Coincident(g31,g5)
    c: Coincident(g31,g22)
    c: Equal(g31,g14)
    c: Equal(g5,g31)
    c: Vertical(g23)
    c: Horizontal(g23,g20)
    c: DistanceY(g8,g4) = 2
    c: Parallel(g21,g24)
    c: PointOnObject(g7,g-2)
    c: DistanceY(g-1,g7) = 2.5
    c: Horizontal(g32)
    c: Coincident(g6,g32)
    c: Coincident(g23,g32)
    c: DistanceY(g6,g5) = 0.4
    c: Vertical(g6,g5)
    c: Vertical(g23,g22)
    c: DistanceY(g6,g5) = 0.1
FEATURE [Sketcher::SketchObject] Sketch225
  MapMode = 5
  Placement = pos=(0,0,0) rot=(1,0,0;1.5708rad)
  Support = -> [XZ_Plane1031]
  sketch-geometry (6):
    g0: ArcOfCircle CenterX=8e-16 CenterY=6.1 CenterZ=0 NormalX=0 NormalY=0 NormalZ=1 AngleXU=0 Radius=2.5 StartAngle=0 EndAngle=1.5708
    g1: LineSegment StartX=2.5 StartY=6.1 StartZ=0 EndX=2.5 EndY=1 EndZ=0
    g2: LineSegment StartX=2.5 StartY=1 StartZ=0 EndX=3 EndY=1 EndZ=0
    g3: LineSegment StartX=3 StartY=1 StartZ=0 EndX=3 EndY=0 EndZ=0
    g4: LineSegment StartX=3 StartY=0 StartZ=0 EndX=0 EndY=0 EndZ=0
    g5: LineSegment StartX=-2e-16 StartY=8.6 StartZ=0 EndX=0 EndY=0 EndZ=0
  constraints (17):
    c: Coincident(g1,g0)
    c: Vertical(g1)
    c: Coincident(g2,g1)
    c: Horizontal(g2)
    c: Coincident(g3,g2)
    c: Vertical(g3)
    c: Coincident(g4,g3)
    c: Coincident(g4,g-1)
    c: Horizontal(g4)
    c: Perpendicular(g0,g-2) = 4.71239
    c: Horizontal(g0,g0)
    c: Radius(g0) = 2.5
    c: DistanceY(g4,g0) = 8.6
    c: DistanceY(g3,g3) = 1
    c: DistanceX(g4,g4) = 3
    c: Coincident(g5,g0)
    c: Coincident(g5,g4)
FEATURE [Sketcher::SketchObject] Sketch226
  MapMode = 5
  Support = -> [XY_Plane1031]
  sketch-geometry (4):
    g0: LineSegment StartX=2.5 StartY=4 StartZ=0 EndX=4.5 EndY=4 EndZ=0
    g1: LineSegment StartX=4.5 StartY=4 StartZ=0 EndX=4.5 EndY=-4 EndZ=0
    g2: LineSegment StartX=4.5 StartY=-4 StartZ=0 EndX=2.5 EndY=-4 EndZ=0
    g3: LineSegment StartX=2.5 StartY=-4 StartZ=0 EndX=2.5 EndY=4 EndZ=0
  constraints (11):
    c: Coincident(g0,g1)
    c: Coincident(g1,g2)
    c: Coincident(g2,g3)
    c: Coincident(g3,g0)
    c: Horizontal(g0)
    c: Horizontal(g2)
    c: Vertical(g1)
    c: DistanceX(g-1,g0) = 2.5
    c: Symmetric(g0,g2,g-1)
    c: DistanceY(g3,g3) = 8
    c: DistanceX(g0,g0) = 2
FEATURE [Sketcher::SketchObject] Sketch228
  MapMode = 5
  Placement = pos=(0,0,0) rot=(1,0,0;1.5708rad)
  Support = -> [XZ_Plane1031]
  sketch-geometry (33):
    g0: LineSegment StartX=-1.47 StartY=-5 StartZ=0 EndX=-1.47 EndY=-4.4 EndZ=0
    g1: LineSegment StartX=-1.47 StartY=-4.4 StartZ=0 EndX=-1.57 EndY=-4.4 EndZ=0
    g2: LineSegment StartX=-1.57 StartY=-4.4 StartZ=0 EndX=-1.57 EndY=-3.4 EndZ=0
    g3: LineSegment StartX=-1.57 StartY=-3.4 StartZ=0 EndX=-1.47 EndY=-3.4 EndZ=0
    g4: LineSegment StartX=-1.47 StartY=-3.4 StartZ=0 EndX=-1.47 EndY=4.5 EndZ=0
    g5: LineSegment StartX=-1.47 StartY=4.5 StartZ=0 EndX=-1.07 EndY=4.5 EndZ=0
    g6: LineSegment StartX=-1.07 StartY=4.4 StartZ=0 EndX=-1.07 EndY=4.1 EndZ=0
    g7: LineSegment StartX=-1.07 StartY=4.1 StartZ=0 EndX=0 EndY=2.5 EndZ=0
    g8: LineSegment StartX=0 StartY=2.5 StartZ=0 EndX=-1.07 EndY=2.5 EndZ=0
    g9: LineSegment StartX=-1.07 StartY=2.5 StartZ=0 EndX=-1.07 EndY=-3.4 EndZ=0
    g10: LineSegment StartX=-1.07 StartY=-3.4 StartZ=0 EndX=-0.97 EndY=-3.4 EndZ=0
    g11: LineSegment StartX=-0.97 StartY=-3.4 StartZ=0 EndX=-0.97 EndY=-4.4 EndZ=0
    g12: LineSegment StartX=-0.97 StartY=-4.4 StartZ=0 EndX=-1.07 EndY=-4.4 EndZ=0
    g13: LineSegment StartX=-1.07 StartY=-4.4 StartZ=0 EndX=-1.07 EndY=-5 EndZ=0
    g14: LineSegment StartX=-1.07 StartY=-5 StartZ=0 EndX=-1.47 EndY=-5 EndZ=0
    g15: LineSegment StartX=1.07 StartY=-5 StartZ=0 EndX=1.47 EndY=-5 EndZ=0
    g16: LineSegment StartX=1.47 StartY=-5 StartZ=0 EndX=1.47 EndY=-4.4 EndZ=0
    g17: LineSegment StartX=1.47 StartY=-4.4 StartZ=0 EndX=1.57 EndY=-4.4 EndZ=0
    g18: LineSegment StartX=1.57 StartY=-4.4 StartZ=0 EndX=1.57 EndY=-3.4 EndZ=0
    g19: LineSegment StartX=1.57 StartY=-3.4 StartZ=0 EndX=1.47 EndY=-3.4 EndZ=0
    g20: LineSegment StartX=1.47 StartY=-3.4 StartZ=0 EndX=1.47 EndY=4.1 EndZ=0
    g21: LineSegment StartX=1.47 StartY=4.1 StartZ=0 EndX=1.2025 EndY=4.5 EndZ=0
    g22: LineSegment StartX=1.2025 StartY=4.5 StartZ=0 EndX=-0.67 EndY=4.5 EndZ=0
    g23: LineSegment StartX=-0.67 StartY=4.4 StartZ=0 EndX=-0.67 EndY=4.1 EndZ=0
    g24: LineSegment StartX=-0.67 StartY=4.1 StartZ=0 EndX=0.4 EndY=2.5 EndZ=0
    g25: LineSegment StartX=0.4 StartY=2.5 StartZ=0 EndX=1.07 EndY=2.5 EndZ=0
    g26: LineSegment StartX=1.07 StartY=2.5 StartZ=0 EndX=1.07 EndY=-3.4 EndZ=0
    g27: LineSegment StartX=1.07 StartY=-3.4 StartZ=0 EndX=0.97 EndY=-3.4 EndZ=0
    g28: LineSegment StartX=0.97 StartY=-3.4 StartZ=0 EndX=0.97 EndY=-4.4 EndZ=0
    g29: LineSegment StartX=0.97 StartY=-4.4 StartZ=0 EndX=1.07 EndY=-4.4 EndZ=0
    g30: LineSegment StartX=1.07 StartY=-4.4 StartZ=0 EndX=1.07 EndY=-5 EndZ=0
    g31: LineSegment StartX=-1.07 StartY=4.5 StartZ=0 EndX=-0.67 EndY=4.5 EndZ=0
    g32: LineSegment StartX=-1.07 StartY=4.4 StartZ=0 EndX=-0.67 EndY=4.4 EndZ=0
  constraints (97):
    c: Vertical(g0)
    c: Coincident(g0,g1)
    c: Horizontal(g1)
    c: Coincident(g1,g2)
    c: Vertical(g2)
    c: Coincident(g2,g3)
    c: Horizontal(g3)
    c: Coincident(g3,g4)
    c: Vertical(g4)
    c: Coincident(g4,g5)
    c: Horizontal(g5)
    c: Vertical(g6)
    c: Coincident(g6,g7)
    c: Coincident(g7,g8)
    c: Horizontal(g8)
    c: Coincident(g8,g9)
    c: Vertical(g9)
    c: Coincident(g9,g10)
    c: Coincident(g10,g11)
    c: Vertical(g11)
    c: Coincident(g11,g12)
    c: Coincident(g12,g13)
    c: Vertical(g13)
    c: Coincident(g13,g14)
    c: Coincident(g14,g0)
    c: Horizontal(g14)
    c: Coincident(g15,g16)
    c: Vertical(g16)
    c: Coincident(g16,g17)
    c: Horizontal(g17)
    c: Coincident(g17,g18)
    c: Vertical(g18)
    c: Coincident(g18,g19)
    c: Horizontal(g19)
    c: Coincident(g19,g20)
    c: Vertical(g20)
    c: Coincident(g20,g21)
    c: Coincident(g21,g22)
    c: Horizontal(g22)
    c: Coincident(g23,g24)
    c: Coincident(g24,g25)
    c: Horizontal(g25)
    c: Coincident(g25,g26)
    c: Vertical(g26)
    c: Coincident(g26,g27)
    c: Horizontal(g27)
    c: Coincident(g27,g28)
    c: Vertical(g28)
    c: Coincident(g28,g29)
    c: Horizontal(g29)
    c: Coincident(g29,g30)
    c: Coincident(g30,g15)
    c: Vertical(g30)
    c: Horizontal(g15)
    c: Horizontal(g5,g22)
    c: Horizontal(g7,g24)
    c: Horizontal(g6,g23)
    c: Parallel(g7,g24)
    c: Equal(g14,g15)
    c: Equal(g18,g2)
    c: Equal(g2,g11)
    c: Equal(g11,g28)
    c: Horizontal(g3,g9)
    c: Horizontal(g9,g26)
    c: Horizontal(g26,g19)
    c: Horizontal(g12)
    c: Vertical(g3,g0)
    c: Vertical(g12,g9)
    c: Vertical(g29,g26)
    c: Vertical(g19,g16)
    c: DistanceX(g0,g15) = 2.54
    c: DistanceX(g28,g17) = 0.6
    c: DistanceX(g1,g11) = 0.6
    c: DistanceX(g15,g15) = 0.4
    c: Symmetric(g13,g15,g-2)
    c: Symmetric(g11,g28,g-2)
    c: Equal(g1,g12)
    c: DistanceY(g11,g11) = 1
    c: DistanceY(g10,g-1) = 3.4
    c: DistanceY(g13,g-1) = 5
    c: Coincident(g31,g5)
    c: Coincident(g31,g22)
    c: Equal(g31,g14)
    c: Equal(g5,g31)
    c: Vertical(g23)
    c: Horizontal(g23,g20)
    c: DistanceY(g8,g4) = 2
    c: Parallel(g21,g24)
    c: PointOnObject(g7,g-2)
    c: DistanceY(g-1,g7) = 2.5
    c: Horizontal(g32)
    c: Coincident(g6,g32)
    c: Coincident(g23,g32)
    c: DistanceY(g6,g5) = 0.4
    c: Vertical(g6,g5)
    c: Vertical(g23,g22)
    c: DistanceY(g6,g5) = 0.1
FEATURE [Sketcher::SketchObject] Sketch229
  MapMode = 5
  Placement = pos=(0,0,0) rot=(1,0,0;1.5708rad)
  Support = -> [XZ_Plane1022]
  sketch-geometry (6):
    g0: ArcOfCircle CenterX=8e-16 CenterY=6.1 CenterZ=0 NormalX=0 NormalY=0 NormalZ=1 AngleXU=0 Radius=2.5 StartAngle=0 EndAngle=1.5708
    g1: LineSegment StartX=2.5 StartY=6.1 StartZ=0 EndX=2.5 EndY=1 EndZ=0
    g2: LineSegment StartX=2.5 StartY=1 StartZ=0 EndX=3 EndY=1 EndZ=0
    g3: LineSegment StartX=3 StartY=1 StartZ=0 EndX=3 EndY=0 EndZ=0
    g4: LineSegment StartX=3 StartY=0 StartZ=0 EndX=0 EndY=0 EndZ=0
    g5: LineSegment StartX=-2e-16 StartY=8.6 StartZ=0 EndX=0 EndY=0 EndZ=0
  constraints (17):
    c: Coincident(g1,g0)
    c: Vertical(g1)
    c: Coincident(g2,g1)
    c: Horizontal(g2)
    c: Coincident(g3,g2)
    c: Vertical(g3)
    c: Coincident(g4,g3)
    c: Coincident(g4,g-1)
    c: Horizontal(g4)
    c: Perpendicular(g0,g-2) = 4.71239
    c: Horizontal(g0,g0)
    c: Radius(g0) = 2.5
    c: DistanceY(g4,g0) = 8.6
    c: DistanceY(g3,g3) = 1
    c: DistanceX(g4,g4) = 3
    c: Coincident(g5,g0)
    c: Coincident(g5,g4)
FEATURE [Sketcher::SketchObject] Sketch223
  MapMode = 5
  Placement = pos=(0,0,0) rot=(1,0,0;1.5708rad)
  Support = -> [XZ_Plane1044]
  sketch-geometry (33):
    g0: LineSegment StartX=-1.47 StartY=-5 StartZ=0 EndX=-1.47 EndY=-4.4 EndZ=0
    g1: LineSegment StartX=-1.47 StartY=-4.4 StartZ=0 EndX=-1.57 EndY=-4.4 EndZ=0
    g2: LineSegment StartX=-1.57 StartY=-4.4 StartZ=0 EndX=-1.57 EndY=-3.4 EndZ=0
    g3: LineSegment StartX=-1.57 StartY=-3.4 StartZ=0 EndX=-1.47 EndY=-3.4 EndZ=0
    g4: LineSegment StartX=-1.47 StartY=-3.4 StartZ=0 EndX=-1.47 EndY=4.5 EndZ=0
    g5: LineSegment StartX=-1.47 StartY=4.5 StartZ=0 EndX=-1.07 EndY=4.5 EndZ=0
    g6: LineSegment StartX=-1.07 StartY=4.4 StartZ=0 EndX=-1.07 EndY=4.1 EndZ=0
    g7: LineSegment StartX=-1.07 StartY=4.1 StartZ=0 EndX=0 EndY=2.5 EndZ=0
    g8: LineSegment StartX=0 StartY=2.5 StartZ=0 EndX=-1.07 EndY=2.5 EndZ=0
    g9: LineSegment StartX=-1.07 StartY=2.5 StartZ=0 EndX=-1.07 EndY=-3.4 EndZ=0
    g10: LineSegment StartX=-1.07 StartY=-3.4 StartZ=0 EndX=-0.97 EndY=-3.4 EndZ=0
    g11: LineSegment StartX=-0.97 StartY=-3.4 StartZ=0 EndX=-0.97 EndY=-4.4 EndZ=0
    g12: LineSegment StartX=-0.97 StartY=-4.4 StartZ=0 EndX=-1.07 EndY=-4.4 EndZ=0
    g13: LineSegment StartX=-1.07 StartY=-4.4 StartZ=0 EndX=-1.07 EndY=-5 EndZ=0
    g14: LineSegment StartX=-1.07 StartY=-5 StartZ=0 EndX=-1.47 EndY=-5 EndZ=0
    g15: LineSegment StartX=1.07 StartY=-5 StartZ=0 EndX=1.47 EndY=-5 EndZ=0
    g16: LineSegment StartX=1.47 StartY=-5 StartZ=0 EndX=1.47 EndY=-4.4 EndZ=0
    g17: LineSegment StartX=1.47 StartY=-4.4 StartZ=0 EndX=1.57 EndY=-4.4 EndZ=0
    g18: LineSegment StartX=1.57 StartY=-4.4 StartZ=0 EndX=1.57 EndY=-3.4 EndZ=0
    g19: LineSegment StartX=1.57 StartY=-3.4 StartZ=0 EndX=1.47 EndY=-3.4 EndZ=0
    g20: LineSegment StartX=1.47 StartY=-3.4 StartZ=0 EndX=1.47 EndY=4.1 EndZ=0
    g21: LineSegment StartX=1.47 StartY=4.1 StartZ=0 EndX=1.2025 EndY=4.5 EndZ=0
    g22: LineSegment StartX=1.2025 StartY=4.5 StartZ=0 EndX=-0.67 EndY=4.5 EndZ=0
    g23: LineSegment StartX=-0.67 StartY=4.4 StartZ=0 EndX=-0.67 EndY=4.1 EndZ=0
    g24: LineSegment StartX=-0.67 StartY=4.1 StartZ=0 EndX=0.4 EndY=2.5 EndZ=0
    g25: LineSegment StartX=0.4 StartY=2.5 StartZ=0 EndX=1.07 EndY=2.5 EndZ=0
    g26: LineSegment StartX=1.07 StartY=2.5 StartZ=0 EndX=1.07 EndY=-3.4 EndZ=0
    g27: LineSegment StartX=1.07 StartY=-3.4 StartZ=0 EndX=0.97 EndY=-3.4 EndZ=0
    g28: LineSegment StartX=0.97 StartY=-3.4 StartZ=0 EndX=0.97 EndY=-4.4 EndZ=0
    g29: LineSegment StartX=0.97 StartY=-4.4 StartZ=0 EndX=1.07 EndY=-4.4 EndZ=0
    g30: LineSegment StartX=1.07 StartY=-4.4 StartZ=0 EndX=1.07 EndY=-5 EndZ=0
    g31: LineSegment StartX=-1.07 StartY=4.5 StartZ=0 EndX=-0.67 EndY=4.5 EndZ=0
    g32: LineSegment StartX=-1.07 StartY=4.4 StartZ=0 EndX=-0.67 EndY=4.4 EndZ=0
  constraints (97):
    c: Vertical(g0)
    c: Coincident(g0,g1)
    c: Horizontal(g1)
    c: Coincident(g1,g2)
    c: Vertical(g2)
    c: Coincident(g2,g3)
    c: Horizontal(g3)
    c: Coincident(g3,g4)
    c: Vertical(g4)
    c: Coincident(g4,g5)
    c: Horizontal(g5)
    c: Vertical(g6)
    c: Coincident(g6,g7)
    c: Coincident(g7,g8)
    c: Horizontal(g8)
    c: Coincident(g8,g9)
    c: Vertical(g9)
    c: Coincident(g9,g10)
    c: Coincident(g10,g11)
    c: Vertical(g11)
    c: Coincident(g11,g12)
    c: Coincident(g12,g13)
    c: Vertical(g13)
    c: Coincident(g13,g14)
    c: Coincident(g14,g0)
    c: Horizontal(g14)
    c: Coincident(g15,g16)
    c: Vertical(g16)
    c: Coincident(g16,g17)
    c: Horizontal(g17)
    c: Coincident(g17,g18)
    c: Vertical(g18)
    c: Coincident(g18,g19)
    c: Horizontal(g19)
    c: Coincident(g19,g20)
    c: Vertical(g20)
    c: Coincident(g20,g21)
    c: Coincident(g21,g22)
    c: Horizontal(g22)
    c: Coincident(g23,g24)
    c: Coincident(g24,g25)
    c: Horizontal(g25)
    c: Coincident(g25,g26)
    c: Vertical(g26)
    c: Coincident(g26,g27)
    c: Horizontal(g27)
    c: Coincident(g27,g28)
    c: Vertical(g28)
    c: Coincident(g28,g29)
    c: Horizontal(g29)
    c: Coincident(g29,g30)
    c: Coincident(g30,g15)
    c: Vertical(g30)
    c: Horizontal(g15)
    c: Horizontal(g5,g22)
    c: Horizontal(g7,g24)
    c: Horizontal(g6,g23)
    c: Parallel(g7,g24)
    c: Equal(g14,g15)
    c: Equal(g18,g2)
    c: Equal(g2,g11)
    c: Equal(g11,g28)
    c: Horizontal(g3,g9)
    c: Horizontal(g9,g26)
    c: Horizontal(g26,g19)
    c: Horizontal(g12)
    c: Vertical(g3,g0)
    c: Vertical(g12,g9)
    c: Vertical(g29,g26)
    c: Vertical(g19,g16)
    c: DistanceX(g0,g15) = 2.54
    c: DistanceX(g28,g17) = 0.6
    c: DistanceX(g1,g11) = 0.6
    c: DistanceX(g15,g15) = 0.4
    c: Symmetric(g13,g15,g-2)
    c: Symmetric(g11,g28,g-2)
    c: Equal(g1,g12)
    c: DistanceY(g11,g11) = 1
    c: DistanceY(g10,g-1) = 3.4
    c: DistanceY(g13,g-1) = 5
    c: Coincident(g31,g5)
    c: Coincident(g31,g22)
    c: Equal(g31,g14)
    c: Equal(g5,g31)
    c: Vertical(g23)
    c: Horizontal(g23,g20)
    c: DistanceY(g8,g4) = 2
    c: Parallel(g21,g24)
    c: PointOnObject(g7,g-2)
    c: DistanceY(g-1,g7) = 2.5
    c: Horizontal(g32)
    c: Coincident(g6,g32)
    c: Coincident(g23,g32)
    c: DistanceY(g6,g5) = 0.4
    c: Vertical(g6,g5)
    c: Vertical(g23,g22)
    c: DistanceY(g6,g5) = 0.1
FEATURE [Sketcher::SketchObject] Sketch222
  MapMode = 5
  Support = -> [XY_Plane056]
  sketch-geometry (4):
    g0: LineSegment StartX=2.5 StartY=4 StartZ=0 EndX=4.5 EndY=4 EndZ=0
    g1: LineSegment StartX=4.5 StartY=4 StartZ=0 EndX=4.5 EndY=-4 EndZ=0
    g2: LineSegment StartX=4.5 StartY=-4 StartZ=0 EndX=2.5 EndY=-4 EndZ=0
    g3: LineSegment StartX=2.5 StartY=-4 StartZ=0 EndX=2.5 EndY=4 EndZ=0
  constraints (11):
    c: Coincident(g0,g1)
    c: Coincident(g1,g2)
    c: Coincident(g2,g3)
    c: Coincident(g3,g0)
    c: Horizontal(g0)
    c: Horizontal(g2)
    c: Vertical(g1)
    c: DistanceX(g-1,g0) = 2.5
    c: Symmetric(g0,g2,g-1)
    c: DistanceY(g3,g3) = 8
    c: DistanceX(g0,g0) = 2
FEATURE [Sketcher::SketchObject] Sketch224
  MapMode = 5
  Placement = pos=(0,0,0) rot=(1,0,0;1.5708rad)
  Support = -> [XZ_Plane056]
  sketch-geometry (33):
    g0: LineSegment StartX=-1.47 StartY=-5 StartZ=0 EndX=-1.47 EndY=-4.4 EndZ=0
    g1: LineSegment StartX=-1.47 StartY=-4.4 StartZ=0 EndX=-1.57 EndY=-4.4 EndZ=0
    g2: LineSegment StartX=-1.57 StartY=-4.4 StartZ=0 EndX=-1.57 EndY=-3.4 EndZ=0
    g3: LineSegment StartX=-1.57 StartY=-3.4 StartZ=0 EndX=-1.47 EndY=-3.4 EndZ=0
    g4: LineSegment StartX=-1.47 StartY=-3.4 StartZ=0 EndX=-1.47 EndY=4.5 EndZ=0
    g5: LineSegment StartX=-1.47 StartY=4.5 StartZ=0 EndX=-1.07 EndY=4.5 EndZ=0
    g6: LineSegment StartX=-1.07 StartY=4.4 StartZ=0 EndX=-1.07 EndY=4.1 EndZ=0
    g7: LineSegment StartX=-1.07 StartY=4.1 StartZ=0 EndX=0 EndY=2.5 EndZ=0
    g8: LineSegment StartX=0 StartY=2.5 StartZ=0 EndX=-1.07 EndY=2.5 EndZ=0
    g9: LineSegment StartX=-1.07 StartY=2.5 StartZ=0 EndX=-1.07 EndY=-3.4 EndZ=0
    g10: LineSegment StartX=-1.07 StartY=-3.4 StartZ=0 EndX=-0.97 EndY=-3.4 EndZ=0
    g11: LineSegment StartX=-0.97 StartY=-3.4 StartZ=0 EndX=-0.97 EndY=-4.4 EndZ=0
    g12: LineSegment StartX=-0.97 StartY=-4.4 StartZ=0 EndX=-1.07 EndY=-4.4 EndZ=0
    g13: LineSegment StartX=-1.07 StartY=-4.4 StartZ=0 EndX=-1.07 EndY=-5 EndZ=0
    g14: LineSegment StartX=-1.07 StartY=-5 StartZ=0 EndX=-1.47 EndY=-5 EndZ=0
    g15: LineSegment StartX=1.07 StartY=-5 StartZ=0 EndX=1.47 EndY=-5 EndZ=0
    g16: LineSegment StartX=1.47 StartY=-5 StartZ=0 EndX=1.47 EndY=-4.4 EndZ=0
    g17: LineSegment StartX=1.47 StartY=-4.4 StartZ=0 EndX=1.57 EndY=-4.4 EndZ=0
    g18: LineSegment StartX=1.57 StartY=-4.4 StartZ=0 EndX=1.57 EndY=-3.4 EndZ=0
    g19: LineSegment StartX=1.57 StartY=-3.4 StartZ=0 EndX=1.47 EndY=-3.4 EndZ=0
    g20: LineSegment StartX=1.47 StartY=-3.4 StartZ=0 EndX=1.47 EndY=4.1 EndZ=0
    g21: LineSegment StartX=1.47 StartY=4.1 StartZ=0 EndX=1.2025 EndY=4.5 EndZ=0
    g22: LineSegment StartX=1.2025 StartY=4.5 StartZ=0 EndX=-0.67 EndY=4.5 EndZ=0
    g23: LineSegment StartX=-0.67 StartY=4.4 StartZ=0 EndX=-0.67 EndY=4.1 EndZ=0
    g24: LineSegment StartX=-0.67 StartY=4.1 StartZ=0 EndX=0.4 EndY=2.5 EndZ=0
    g25: LineSegment StartX=0.4 StartY=2.5 StartZ=0 EndX=1.07 EndY=2.5 EndZ=0
    g26: LineSegment StartX=1.07 StartY=2.5 StartZ=0 EndX=1.07 EndY=-3.4 EndZ=0
    g27: LineSegment StartX=1.07 StartY=-3.4 StartZ=0 EndX=0.97 EndY=-3.4 EndZ=0
    g28: LineSegment StartX=0.97 StartY=-3.4 StartZ=0 EndX=0.97 EndY=-4.4 EndZ=0
    g29: LineSegment StartX=0.97 StartY=-4.4 StartZ=0 EndX=1.07 EndY=-4.4 EndZ=0
    g30: LineSegment StartX=1.07 StartY=-4.4 StartZ=0 EndX=1.07 EndY=-5 EndZ=0
    g31: LineSegment StartX=-1.07 StartY=4.5 StartZ=0 EndX=-0.67 EndY=4.5 EndZ=0
    g32: LineSegment StartX=-1.07 StartY=4.4 StartZ=0 EndX=-0.67 EndY=4.4 EndZ=0
  constraints (97):
    c: Vertical(g0)
    c: Coincident(g0,g1)
    c: Horizontal(g1)
    c: Coincident(g1,g2)
    c: Vertical(g2)
    c: Coincident(g2,g3)
    c: Horizontal(g3)
    c: Coincident(g3,g4)
    c: Vertical(g4)
    c: Coincident(g4,g5)
    c: Horizontal(g5)
    c: Vertical(g6)
    c: Coincident(g6,g7)
    c: Coincident(g7,g8)
    c: Horizontal(g8)
    c: Coincident(g8,g9)
    c: Vertical(g9)
    c: Coincident(g9,g10)
    c: Coincident(g10,g11)
    c: Vertical(g11)
    c: Coincident(g11,g12)
    c: Coincident(g12,g13)
    c: Vertical(g13)
    c: Coincident(g13,g14)
    c: Coincident(g14,g0)
    c: Horizontal(g14)
    c: Coincident(g15,g16)
    c: Vertical(g16)
    c: Coincident(g16,g17)
    c: Horizontal(g17)
    c: Coincident(g17,g18)
    c: Vertical(g18)
    c: Coincident(g18,g19)
    c: Horizontal(g19)
    c: Coincident(g19,g20)
    c: Vertical(g20)
    c: Coincident(g20,g21)
    c: Coincident(g21,g22)
    c: Horizontal(g22)
    c: Coincident(g23,g24)
    c: Coincident(g24,g25)
    c: Horizontal(g25)
    c: Coincident(g25,g26)
    c: Vertical(g26)
    c: Coincident(g26,g27)
    c: Horizontal(g27)
    c: Coincident(g27,g28)
    c: Vertical(g28)
    c: Coincident(g28,g29)
    c: Horizontal(g29)
    c: Coincident(g29,g30)
    c: Coincident(g30,g15)
    c: Vertical(g30)
    c: Horizontal(g15)
    c: Horizontal(g5,g22)
    c: Horizontal(g7,g24)
    c: Horizontal(g6,g23)
    c: Parallel(g7,g24)
    c: Equal(g14,g15)
    c: Equal(g18,g2)
    c: Equal(g2,g11)
    c: Equal(g11,g28)
    c: Horizontal(g3,g9)
    c: Horizontal(g9,g26)
    c: Horizontal(g26,g19)
    c: Horizontal(g12)
    c: Vertical(g3,g0)
    c: Vertical(g12,g9)
    c: Vertical(g29,g26)
    c: Vertical(g19,g16)
    c: DistanceX(g0,g15) = 2.54
    c: DistanceX(g28,g17) = 0.6
    c: DistanceX(g1,g11) = 0.6
    c: DistanceX(g15,g15) = 0.4
    c: Symmetric(g13,g15,g-2)
    c: Symmetric(g11,g28,g-2)
    c: Equal(g1,g12)
    c: DistanceY(g11,g11) = 1
    c: DistanceY(g10,g-1) = 3.4
    c: DistanceY(g13,g-1) = 5
    c: Coincident(g31,g5)
    c: Coincident(g31,g22)
    c: Equal(g31,g14)
    c: Equal(g5,g31)
    c: Vertical(g23)
    c: Horizontal(g23,g20)
    c: DistanceY(g8,g4) = 2
    c: Parallel(g21,g24)
    c: PointOnObject(g7,g-2)
    c: DistanceY(g-1,g7) = 2.5
    c: Horizontal(g32)
    c: Coincident(g6,g32)
    c: Coincident(g23,g32)
    c: DistanceY(g6,g5) = 0.4
    c: Vertical(g6,g5)
    c: Vertical(g23,g22)
    c: DistanceY(g6,g5) = 0.1
FEATURE [Sketcher::SketchObject] Sketch231
  MapMode = 5
  Placement = pos=(0,0,0) rot=(1,0,0;1.5708rad)
  Support = -> [XZ_Plane1020]
  sketch-geometry (33):
    g0: LineSegment StartX=-1.47 StartY=-5 StartZ=0 EndX=-1.47 EndY=-4.4 EndZ=0
    g1: LineSegment StartX=-1.47 StartY=-4.4 StartZ=0 EndX=-1.57 EndY=-4.4 EndZ=0
    g2: LineSegment StartX=-1.57 StartY=-4.4 StartZ=0 EndX=-1.57 EndY=-3.4 EndZ=0
    g3: LineSegment StartX=-1.57 StartY=-3.4 StartZ=0 EndX=-1.47 EndY=-3.4 EndZ=0
    g4: LineSegment StartX=-1.47 StartY=-3.4 StartZ=0 EndX=-1.47 EndY=4.5 EndZ=0
    g5: LineSegment StartX=-1.47 StartY=4.5 StartZ=0 EndX=-1.07 EndY=4.5 EndZ=0
    g6: LineSegment StartX=-1.07 StartY=4.4 StartZ=0 EndX=-1.07 EndY=4.1 EndZ=0
    g7: LineSegment StartX=-1.07 StartY=4.1 StartZ=0 EndX=0 EndY=2.5 EndZ=0
    g8: LineSegment StartX=0 StartY=2.5 StartZ=0 EndX=-1.07 EndY=2.5 EndZ=0
    g9: LineSegment StartX=-1.07 StartY=2.5 StartZ=0 EndX=-1.07 EndY=-3.4 EndZ=0
    g10: LineSegment StartX=-1.07 StartY=-3.4 StartZ=0 EndX=-0.97 EndY=-3.4 EndZ=0
    g11: LineSegment StartX=-0.97 StartY=-3.4 StartZ=0 EndX=-0.97 EndY=-4.4 EndZ=0
    g12: LineSegment StartX=-0.97 StartY=-4.4 StartZ=0 EndX=-1.07 EndY=-4.4 EndZ=0
    g13: LineSegment StartX=-1.07 StartY=-4.4 StartZ=0 EndX=-1.07 EndY=-5 EndZ=0
    g14: LineSegment StartX=-1.07 StartY=-5 StartZ=0 EndX=-1.47 EndY=-5 EndZ=0
    g15: LineSegment StartX=1.07 StartY=-5 StartZ=0 EndX=1.47 EndY=-5 EndZ=0
    g16: LineSegment StartX=1.47 StartY=-5 StartZ=0 EndX=1.47 EndY=-4.4 EndZ=0
    g17: LineSegment StartX=1.47 StartY=-4.4 StartZ=0 EndX=1.57 EndY=-4.4 EndZ=0
    g18: LineSegment StartX=1.57 StartY=-4.4 StartZ=0 EndX=1.57 EndY=-3.4 EndZ=0
    g19: LineSegment StartX=1.57 StartY=-3.4 StartZ=0 EndX=1.47 EndY=-3.4 EndZ=0
    g20: LineSegment StartX=1.47 StartY=-3.4 StartZ=0 EndX=1.47 EndY=4.1 EndZ=0
    g21: LineSegment StartX=1.47 StartY=4.1 StartZ=0 EndX=1.2025 EndY=4.5 EndZ=0
    g22: LineSegment StartX=1.2025 StartY=4.5 StartZ=0 EndX=-0.67 EndY=4.5 EndZ=0
    g23: LineSegment StartX=-0.67 StartY=4.4 StartZ=0 EndX=-0.67 EndY=4.1 EndZ=0
    g24: LineSegment StartX=-0.67 StartY=4.1 StartZ=0 EndX=0.4 EndY=2.5 EndZ=0
    g25: LineSegment StartX=0.4 StartY=2.5 StartZ=0 EndX=1.07 EndY=2.5 EndZ=0
    g26: LineSegment StartX=1.07 StartY=2.5 StartZ=0 EndX=1.07 EndY=-3.4 EndZ=0
    g27: LineSegment StartX=1.07 StartY=-3.4 StartZ=0 EndX=0.97 EndY=-3.4 EndZ=0
    g28: LineSegment StartX=0.97 StartY=-3.4 StartZ=0 EndX=0.97 EndY=-4.4 EndZ=0
    g29: LineSegment StartX=0.97 StartY=-4.4 StartZ=0 EndX=1.07 EndY=-4.4 EndZ=0
    g30: LineSegment StartX=1.07 StartY=-4.4 StartZ=0 EndX=1.07 EndY=-5 EndZ=0
    g31: LineSegment StartX=-1.07 StartY=4.5 StartZ=0 EndX=-0.67 EndY=4.5 EndZ=0
    g32: LineSegment StartX=-1.07 StartY=4.4 StartZ=0 EndX=-0.67 EndY=4.4 EndZ=0
  constraints (97):
    c: Vertical(g0)
    c: Coincident(g0,g1)
    c: Horizontal(g1)
    c: Coincident(g1,g2)
    c: Vertical(g2)
    c: Coincident(g2,g3)
    c: Horizontal(g3)
    c: Coincident(g3,g4)
    c: Vertical(g4)
    c: Coincident(g4,g5)
    c: Horizontal(g5)
    c: Vertical(g6)
    c: Coincident(g6,g7)
    c: Coincident(g7,g8)
    c: Horizontal(g8)
    c: Coincident(g8,g9)
    c: Vertical(g9)
    c: Coincident(g9,g10)
    c: Coincident(g10,g11)
    c: Vertical(g11)
    c: Coincident(g11,g12)
    c: Coincident(g12,g13)
    c: Vertical(g13)
    c: Coincident(g13,g14)
    c: Coincident(g14,g0)
    c: Horizontal(g14)
    c: Coincident(g15,g16)
    c: Vertical(g16)
    c: Coincident(g16,g17)
    c: Horizontal(g17)
    c: Coincident(g17,g18)
    c: Vertical(g18)
    c: Coincident(g18,g19)
    c: Horizontal(g19)
    c: Coincident(g19,g20)
    c: Vertical(g20)
    c: Coincident(g20,g21)
    c: Coincident(g21,g22)
    c: Horizontal(g22)
    c: Coincident(g23,g24)
    c: Coincident(g24,g25)
    c: Horizontal(g25)
    c: Coincident(g25,g26)
    c: Vertical(g26)
    c: Coincident(g26,g27)
    c: Horizontal(g27)
    c: Coincident(g27,g28)
    c: Vertical(g28)
    c: Coincident(g28,g29)
    c: Horizontal(g29)
    c: Coincident(g29,g30)
    c: Coincident(g30,g15)
    c: Vertical(g30)
    c: Horizontal(g15)
    c: Horizontal(g5,g22)
    c: Horizontal(g7,g24)
    c: Horizontal(g6,g23)
    c: Parallel(g7,g24)
    c: Equal(g14,g15)
    c: Equal(g18,g2)
    c: Equal(g2,g11)
    c: Equal(g11,g28)
    c: Horizontal(g3,g9)
    c: Horizontal(g9,g26)
    c: Horizontal(g26,g19)
    c: Horizontal(g12)
    c: Vertical(g3,g0)
    c: Vertical(g12,g9)
    c: Vertical(g29,g26)
    c: Vertical(g19,g16)
    c: DistanceX(g0,g15) = 2.54
    c: DistanceX(g28,g17) = 0.6
    c: DistanceX(g1,g11) = 0.6
    c: DistanceX(g15,g15) = 0.4
    c: Symmetric(g13,g15,g-2)
    c: Symmetric(g11,g28,g-2)
    c: Equal(g1,g12)
    c: DistanceY(g11,g11) = 1
    c: DistanceY(g10,g-1) = 3.4
    c: DistanceY(g13,g-1) = 5
    c: Coincident(g31,g5)
    c: Coincident(g31,g22)
    c: Equal(g31,g14)
    c: Equal(g5,g31)
    c: Vertical(g23)
    c: Horizontal(g23,g20)
    c: DistanceY(g8,g4) = 2
    c: Parallel(g21,g24)
    c: PointOnObject(g7,g-2)
    c: DistanceY(g-1,g7) = 2.5
    c: Horizontal(g32)
    c: Coincident(g6,g32)
    c: Coincident(g23,g32)
    c: DistanceY(g6,g5) = 0.4
    c: Vertical(g6,g5)
    c: Vertical(g23,g22)
    c: DistanceY(g6,g5) = 0.1
FEATURE [Sketcher::SketchObject] Sketch2452
  MapMode = 5
  Support = -> [XY_Plane1077]
  sketch-geometry (1):
    g0: Circle CenterX=0 CenterY=0 CenterZ=0 NormalX=0 NormalY=0 NormalZ=1 AngleXU=0 Radius=2.75
  constraints (2):
    c: Coincident(g0,g-1)
    c: Radius(g0) = 2.75
FEATURE [Sketcher::SketchObject] Sketch2459
  MapMode = 5
  Support = -> [XY_Plane1079]
  sketch-geometry (1):
    g0: Circle CenterX=0 CenterY=0 CenterZ=0 NormalX=0 NormalY=0 NormalZ=1 AngleXU=0 Radius=2.75
  constraints (2):
    c: Coincident(g0,g-1)
    c: Radius(g0) = 2.75
FEATURE [Sketcher::SketchObject] Sketch2460
  MapMode = 5
  Support = -> [XY_Plane1064]
  sketch-geometry (1):
    g0: Circle CenterX=0 CenterY=0 CenterZ=0 NormalX=0 NormalY=0 NormalZ=1 AngleXU=0 Radius=2.75
  constraints (2):
    c: Coincident(g0,g-1)
    c: Radius(g0) = 2.75
FEATURE [Sketcher::SketchObject] Sketch2462
  MapMode = 5
  Support = -> [XY_Plane1067]
  sketch-geometry (1):
    g0: Circle CenterX=0 CenterY=0 CenterZ=0 NormalX=0 NormalY=0 NormalZ=1 AngleXU=0 Radius=2.75
  constraints (2):
    c: Coincident(g0,g-1)
    c: Radius(g0) = 2.75
FEATURE [Sketcher::SketchObject] Sketch2465
  MapMode = 5
  Support = -> [XY_Plane1053]
  sketch-geometry (4):
    g0: LineSegment StartX=-1.27 StartY=-1.27 StartZ=0 EndX=1.27 EndY=-1.27 EndZ=0
    g1: LineSegment StartX=1.27 StartY=-1.27 StartZ=0 EndX=1.27 EndY=1.27 EndZ=0
    g2: LineSegment StartX=1.27 StartY=1.27 StartZ=0 EndX=-1.27 EndY=1.27 EndZ=0
    g3: LineSegment StartX=-1.27 StartY=1.27 StartZ=0 EndX=-1.27 EndY=-1.27 EndZ=0
  constraints (10):
    c: Coincident(g0,g1)
    c: Coincident(g1,g2)
    c: Coincident(g2,g3)
    c: Coincident(g3,g0)
    c: Horizontal(g0)
    c: Vertical(g3)
    c: Symmetric(g1,g2,g-2)
    c: Symmetric(g0,g1,g-1)
    c: Equal(g3,g2)
    c: DistanceX(g2,g2) = 2.54
FEATURE [Sketcher::SketchObject] Sketch2466
  AttachmentOffset = pos=(0,0,42) rot=(0,0,1;0rad)
  MapMode = 5
  Placement = pos=(0,0,42) rot=(0,0,1;0rad)
  Support = -> [XY_Plane1007]
  sketch-geometry (8):
    g0: ArcOfCircle CenterX=25 CenterY=0.35 CenterZ=0 NormalX=0 NormalY=0 NormalZ=1 AngleXU=0 Radius=15 StartAngle=3.14159 EndAngle=4.71239
    g1: LineSegment StartX=25 StartY=-14.65 StartZ=0 EndX=89 EndY=-14.65 EndZ=0
    g2: ArcOfCircle CenterX=89 CenterY=0.35 CenterZ=0 NormalX=0 NormalY=0 NormalZ=1 AngleXU=0 Radius=15 StartAngle=4.71239 EndAngle=6.28319
    g3: ArcOfCircle CenterX=25 CenterY=34.05 CenterZ=0 NormalX=0 NormalY=0 NormalZ=1 AngleXU=0 Radius=15 StartAngle=1.5708 EndAngle=3.14159
    g4: LineSegment StartX=25 StartY=49.05 StartZ=0 EndX=89 EndY=49.05 EndZ=0
    g5: LineSegment StartX=10 StartY=34.05 StartZ=0 EndX=10 EndY=0.35 EndZ=0
    g6: ArcOfCircle CenterX=89 CenterY=34.05 CenterZ=0 NormalX=0 NormalY=0 NormalZ=1 AngleXU=0 Radius=15 StartAngle=0 EndAngle=1.5708
    g7: LineSegment StartX=104 StartY=34.05 StartZ=0 EndX=104 EndY=0.35 EndZ=0
  constraints (21):
    c: Horizontal(g1)
    c: Tangent(g1,g0) = -1.5708
    c: Angle(g0) = 1.5708
    c: DistanceX(g-1,g0) = 25
    c: DistanceX(g1,g1) = 64
    c: Equal(g0,g2)
    c: DistanceY(g0,g-1) = 14.65
    c: Horizontal(g4)
    c: Vertical(g0,g3)
    c: Vertical(g4,g1)
    c: Tangent(g2,g1) = -1.5708
    c: Tangent(g4,g3) = 1.5708
    c: Vertical(g5)
    c: Coincident(g5,g0)
    c: Tangent(g5,g3) = -1.5708
    c: DistanceY(g0,g3) = 63.7
    c: Vertical(g7)
    c: Tangent(g7,g2) = 1.5708
    c: Tangent(g7,g6) = 1.5708
    c: Tangent(g6,g4) = 1.5708
    c: DistanceX(g-1,g0) = 10
FEATURE [Sketcher::SketchObject] Sketch2467
  AttachmentOffset = pos=(0,0,57) rot=(0,0,1;0rad)
  MapMode = 5
  Placement = pos=(57,-1.27e-14,1.27e-14) rot=(0.57735,0.57735,0.57735;2.0944rad)
  Support = -> [YZ_Plane1001]
  sketch-geometry (3):
    g0: LineSegment StartX=-14.65 StartY=44 StartZ=0 EndX=49.05 EndY=44 EndZ=0
    g1: LineSegment StartX=49.05 StartY=44 StartZ=0 EndX=49.05 EndY=72.9546 EndZ=0
    g2: LineSegment StartX=49.05 StartY=72.9546 StartZ=0 EndX=-14.65 EndY=44 EndZ=0
  constraints (9):
    c: Horizontal(g0)
    c: Coincident(g0,g1)
    c: Vertical(g1)
    c: Coincident(g1,g2)
    c: Coincident(g2,g0)
    c: Angle(g0,g2) = 0.426628
    c: DistanceY(g-1,g0) = 44
    c: DistanceX(g0,g-1) = 14.65
    c: DistanceX(g0,g0) = 63.7
FEATURE [Sketcher::SketchObject] Sketch2475
  AttachmentOffset = pos=(0,0,-29) rot=(0,0,1;0rad)
  MapMode = 5
  Placement = pos=(0,29,6.4e-15) rot=(1,0,0;1.5708rad)
  Support = -> [XZ_Plane1006]
  sketch-geometry (6):
    g0: LineSegment StartX=39 StartY=47 StartZ=0 EndX=39 EndY=52 EndZ=0
    g1: LineSegment StartX=39 StartY=52 StartZ=0 EndX=36.8349 EndY=50.75 EndZ=0
    g2: LineSegment StartX=36.8349 StartY=50.75 StartZ=0 EndX=39 EndY=47 EndZ=0
    g3: LineSegment StartX=75 StartY=52 StartZ=0 EndX=75 EndY=47 EndZ=0
    g4: LineSegment StartX=75 StartY=47 StartZ=0 EndX=77.1651 EndY=50.75 EndZ=0
    g5: LineSegment StartX=77.1651 StartY=50.75 StartZ=0 EndX=75 EndY=52 EndZ=0
  constraints (18):
    c: Vertical(g0)
    c: Coincident(g0,g1)
    c: Coincident(g1,g2)
    c: Coincident(g2,g0)
    c: Vertical(g3)
    c: Coincident(g3,g4)
    c: Coincident(g4,g5)
    c: Coincident(g5,g3)
    c: Equal(g0,g3)
    c: Equal(g5,g1)
    c: Equal(g2,g4)
    c: Perpendicular(g5,g4)
    c: Horizontal(g3,g0)
    c: DistanceX(g0,g3) = 36
    c: DistanceX(g-1,g0) = 39
    c: DistanceY(g-1,g0) = 47
    c: Angle(g3,g5) = 1.0472
    c: DistanceY(g3,g3) = 5
FEATURE [Sketcher::SketchObject] Sketch2483
  AttachmentOffset = pos=(0,0,44.25) rot=(0,0,1;0rad)
  MapMode = 5
  Placement = pos=(0,0,44.25) rot=(0,0,1;0rad)
  Support = -> [XY_Plane1015]
  sketch-geometry (8):
    g0: LineSegment StartX=25 StartY=4 StartZ=0 EndX=89 EndY=4 EndZ=0
    g1: LineSegment StartX=96 StartY=11 StartZ=0 EndX=96 EndY=55 EndZ=0
    g2: LineSegment StartX=89 StartY=62 StartZ=0 EndX=25 EndY=62 EndZ=0
    g3: LineSegment StartX=18 StartY=55 StartZ=0 EndX=18 EndY=11 EndZ=0
    g4: ArcOfCircle CenterX=25 CenterY=55 CenterZ=0 NormalX=0 NormalY=0 NormalZ=1 AngleXU=0 Radius=7 StartAngle=1.5708 EndAngle=3.14159
    g5: ArcOfCircle CenterX=89 CenterY=55 CenterZ=0 NormalX=0 NormalY=0 NormalZ=1 AngleXU=0 Radius=7 StartAngle=0 EndAngle=1.5708
    g6: ArcOfCircle CenterX=89 CenterY=11 CenterZ=0 NormalX=0 NormalY=0 NormalZ=1 AngleXU=0 Radius=7 StartAngle=4.71239 EndAngle=6.28319
    g7: ArcOfCircle CenterX=25 CenterY=11 CenterZ=0 NormalX=0 NormalY=0 NormalZ=1 AngleXU=0 Radius=7 StartAngle=3.14159 EndAngle=4.71239
  constraints (20):
    c: Horizontal(g0)
    c: Horizontal(g2)
    c: Vertical(g1)
    c: Vertical(g3)
    c: Tangent(g3,g4) = -1.5708
    c: Tangent(g2,g4) = -1.5708
    c: Tangent(g2,g5) = -1.5708
    c: Tangent(g1,g5) = -1.5708
    c: Tangent(g1,g6) = -1.5708
    c: Tangent(g0,g6) = -1.5708
    c: Tangent(g0,g7) = -1.5708
    c: Tangent(g3,g7) = -1.5708
    c: Radius(g4) = 7
    c: Equal(g4,g5)
    c: Equal(g5,g6)
    c: Equal(g6,g7)
    c: DistanceX(g3,g1) = 78
    c: DistanceY(g0,g2) = 58
    c: DistanceX(g-1,g7) = 25
    c: DistanceY(g-1,g7) = 11
FEATURE [Sketcher::SketchObject] Sketch2485
  MapMode = 5
  Support = -> [XY_Plane1015]
  sketch-geometry (8):
    g0: ArcOfCircle CenterX=25 CenterY=11 CenterZ=0 NormalX=0 NormalY=0 NormalZ=1 AngleXU=0 Radius=4.5 StartAngle=3.14159 EndAngle=4.71239
    g1: ArcOfCircle CenterX=25 CenterY=55 CenterZ=0 NormalX=0 NormalY=0 NormalZ=1 AngleXU=0 Radius=4.5 StartAngle=1.5708 EndAngle=3.14159
    g2: ArcOfCircle CenterX=89 CenterY=55 CenterZ=0 NormalX=0 NormalY=0 NormalZ=1 AngleXU=0 Radius=4.5 StartAngle=7e-16 EndAngle=1.5708
    g3: ArcOfCircle CenterX=89 CenterY=11 CenterZ=0 NormalX=0 NormalY=0 NormalZ=1 AngleXU=0 Radius=4.5 StartAngle=4.71239 EndAngle=6.28319
    g4: LineSegment StartX=25 StartY=59.5 StartZ=0 EndX=89 EndY=59.5 EndZ=0
    g5: LineSegment StartX=20.5 StartY=55 StartZ=0 EndX=20.5 EndY=11 EndZ=0
    g6: LineSegment StartX=25 StartY=6.5 StartZ=0 EndX=89 EndY=6.5 EndZ=0
    g7: LineSegment StartX=93.5 StartY=11 StartZ=0 EndX=93.5 EndY=55 EndZ=0
  constraints (20):
    c: Horizontal(g4)
    c: Vertical(g5)
    c: Horizontal(g6)
    c: Vertical(g7)
    c: Equal(g1,g2)
    c: Equal(g2,g3)
    c: Equal(g3,g0)
    c: Radius(g2) = 4.5
    c: Tangent(g7,g2) = -1.5708
    c: Tangent(g1,g4) = 1.5708
    c: Tangent(g5,g1) = -1.5708
    c: Tangent(g4,g2) = 1.5708
    c: Tangent(g7,g3) = -1.5708
    c: Tangent(g6,g3) = -1.5708
    c: Tangent(g5,g0) = -1.5708
    c: Tangent(g6,g0) = -1.5708
    c: DistanceX(g4,g4) = 64
    c: DistanceY(g7,g7) = 44
    c: DistanceX(g-1,g0) = 25
    c: DistanceY(g-1,g0) = 11
FEATURE [Sketcher::SketchObject] Sketch2487
  MapMode = 5
  Support = -> [XY_Plane1015]
  sketch-geometry (14):
    g0: Circle CenterX=57 CenterY=33 CenterZ=0 NormalX=0 NormalY=0 NormalZ=1 AngleXU=0 Radius=7.5
    g1: LineSegment [constr] StartX=48 StartY=48.5885 StartZ=0 EndX=39 EndY=33 EndZ=0
    g2: LineSegment [constr] StartX=39 StartY=33 StartZ=0 EndX=48 EndY=17.4115 EndZ=0
    g3: LineSegment [constr] StartX=48 StartY=17.4115 StartZ=0 EndX=66 EndY=17.4115 EndZ=0
    g4: LineSegment [constr] StartX=66 StartY=17.4115 StartZ=0 EndX=75 EndY=33 EndZ=0
    g5: LineSegment [constr] StartX=75 StartY=33 StartZ=0 EndX=66 EndY=48.5885 EndZ=0
    g6: LineSegment [constr] StartX=66 StartY=48.5885 StartZ=0 EndX=48 EndY=48.5885 EndZ=0
    g7: Circle [constr] CenterX=57 CenterY=33 CenterZ=0 NormalX=0 NormalY=0 NormalZ=1 AngleXU=0 Radius=18
    g8: Circle CenterX=48 CenterY=48.5885 CenterZ=0 NormalX=0 NormalY=0 NormalZ=1 AngleXU=0 Radius=2.75
    g9: Circle CenterX=66 CenterY=48.5885 CenterZ=0 NormalX=0 NormalY=0 NormalZ=1 AngleXU=0 Radius=2.75
    g10: Circle CenterX=75 CenterY=33 CenterZ=0 NormalX=0 NormalY=0 NormalZ=1 AngleXU=0 Radius=2.75
    g11: Circle CenterX=39 CenterY=33 CenterZ=0 NormalX=0 NormalY=0 NormalZ=1 AngleXU=0 Radius=2.75
    g12: Circle CenterX=48 CenterY=17.4115 CenterZ=0 NormalX=0 NormalY=0 NormalZ=1 AngleXU=0 Radius=2.75
    g13: Circle CenterX=66 CenterY=17.4115 CenterZ=0 NormalX=0 NormalY=0 NormalZ=1 AngleXU=0 Radius=2.75
  constraints (31):
    c: DistanceY(g-1,g0) = 33
    c: DistanceX(g-1,g0) = 57
    c: Radius(g0) = 7.5
    c: Coincident(g1,g2)
    c: Coincident(g2,g3)
    c: Coincident(g3,g4)
    c: Coincident(g4,g5)
    c: Coincident(g5,g6)
    c: Coincident(g6,g1)
    c: Equal(g1, g2-g6) x5
    c: PointOnObject(g1,g7)
    c: PointOnObject(g2,g7)
    c: PointOnObject(g3,g7)
    c: PointOnObject(g4,g7)
    c: PointOnObject(g5,g7)
    c: PointOnObject(g6,g7)
    c: Coincident(g7,g0)
    c: DistanceX(g6,g6) = 18
    c: Coincident(g8,g1)
    c: Coincident(g9,g5)
    c: Coincident(g10,g4)
    c: Coincident(g11,g1)
    c: Coincident(g12,g2)
    c: Coincident(g13,g3)
    c: Equal(g10,g9)
    c: Equal(g9,g8)
    c: Equal(g8,g11)
    c: Equal(g11,g12)
    c: Equal(g12,g13)
    c: Radius(g10) = 2.75
    c: Horizontal(g6)
FEATURE [Sketcher::SketchObject] Sketch2489
  AttachmentOffset = pos=(0,0,32) rot=(0,0,1;0rad)
  MapMode = 5
  Placement = pos=(0,0,32) rot=(0,0,1;0rad)
  Support = -> [XY_Plane1015]
  sketch-geometry (9):
    g0: LineSegment [constr] StartX=66 StartY=48.5885 StartZ=0 EndX=48 EndY=48.5885 EndZ=0
    g1: LineSegment [constr] StartX=48 StartY=48.5885 StartZ=0 EndX=39 EndY=33 EndZ=0
    g2: LineSegment [constr] StartX=39 StartY=33 StartZ=0 EndX=48 EndY=17.4115 EndZ=0
    g3: LineSegment [constr] StartX=48 StartY=17.4115 StartZ=0 EndX=66 EndY=17.4115 EndZ=0
    g4: LineSegment [constr] StartX=66 StartY=17.4115 StartZ=0 EndX=75 EndY=33 EndZ=0
    g5: LineSegment [constr] StartX=75 StartY=33 StartZ=0 EndX=66 EndY=48.5885 EndZ=0
    g6: Circle [constr] CenterX=57 CenterY=33 CenterZ=0 NormalX=0 NormalY=0 NormalZ=1 AngleXU=0 Radius=18
    g7: Circle CenterX=39 CenterY=33 CenterZ=0 NormalX=0 NormalY=0 NormalZ=1 AngleXU=0 Radius=3.2
    g8: Circle CenterX=75 CenterY=33 CenterZ=0 NormalX=0 NormalY=0 NormalZ=1 AngleXU=0 Radius=3.2
  constraints (21):
    c: Coincident(g0,g1)
    c: Coincident(g1,g2)
    c: Coincident(g2,g3)
    c: Coincident(g3,g4)
    c: Coincident(g4,g5)
    c: Coincident(g5,g0)
    c: Equal(g0, g1-g5) x5
    c: PointOnObject(g0,g6)
    c: PointOnObject(g1,g6)
    c: PointOnObject(g2,g6)
    c: PointOnObject(g3,g6)
    c: PointOnObject(g4,g6)
    c: PointOnObject(g5,g6)
    c: Horizontal(g0)
    c: DistanceX(g0,g0) = 18
    c: DistanceX(g-1,g6) = 57
    c: DistanceY(g-1,g6) = 33
    c: Coincident(g7,g1)
    c: Coincident(g8,g4)
    c: Radius(g8) = 3.2
    c: Equal(g8,g7)
FEATURE [Sketcher::SketchObject] Sketch2490
  MapMode = 5
  Placement = pos=(0,0,0) rot=(0.57735,0.57735,0.57735;2.0944rad)
  Support = -> [YZ_Plane1009]
  sketch-geometry (3):
    g0: LineSegment StartX=66 StartY=0 StartZ=0 EndX=76 EndY=45 EndZ=0
    g1: LineSegment StartX=76 StartY=45 StartZ=0 EndX=76 EndY=0 EndZ=0
    g2: LineSegment StartX=76 StartY=0 StartZ=0 EndX=66 EndY=0 EndZ=0
  constraints (9):
    c: PointOnObject(g0,g-1)
    c: Coincident(g0,g1)
    c: PointOnObject(g1,g-1)
    c: Vertical(g1)
    c: Coincident(g1,g2)
    c: Coincident(g2,g0)
    c: DistanceX(g-1,g0) = 66
    c: DistanceX(g2,g2) = 10
    c: DistanceY(g1,g1) = 45
FEATURE [Sketcher::SketchObject] Sketch2494
  AttachmentOffset = pos=(0,0,40) rot=(0,0,1;0rad)
  MapMode = 5
  Placement = pos=(0,0,40) rot=(0,0,1;0rad)
  Support = -> [XY_Plane1015]
  sketch-geometry (24):
    g0: LineSegment StartX=18 StartY=17.4 StartZ=0 EndX=20 EndY=17.4 EndZ=0
    g1: LineSegment StartX=20.5 StartY=17.9 StartZ=0 EndX=20.5 EndY=26.9 EndZ=0
    g2: LineSegment StartX=20 StartY=27.4 StartZ=0 EndX=18 EndY=27.4 EndZ=0
    g3: LineSegment StartX=18 StartY=27.4 StartZ=0 EndX=18 EndY=17.4 EndZ=0
    g4: LineSegment StartX=18 StartY=43 StartZ=0 EndX=20 EndY=43 EndZ=0
    g5: LineSegment StartX=20.5 StartY=43.5 StartZ=0 EndX=20.5 EndY=52.5 EndZ=0
    g6: LineSegment StartX=20 StartY=53 StartZ=0 EndX=18 EndY=53 EndZ=0
    g7: LineSegment StartX=18 StartY=53 StartZ=0 EndX=18 EndY=43 EndZ=0
    g8: LineSegment StartX=96 StartY=53 StartZ=0 EndX=94 EndY=53 EndZ=0
    g9: LineSegment StartX=93.5 StartY=52.5 StartZ=0 EndX=93.5 EndY=43.5 EndZ=0
    g10: LineSegment StartX=94 StartY=43 StartZ=0 EndX=96 EndY=43 EndZ=0
    g11: LineSegment StartX=96 StartY=43 StartZ=0 EndX=96 EndY=53 EndZ=0
    g12: LineSegment StartX=96 StartY=17.4 StartZ=0 EndX=94 EndY=17.4 EndZ=0
    g13: LineSegment StartX=93.5 StartY=17.9 StartZ=0 EndX=93.5 EndY=26.9 EndZ=0
    g14: LineSegment StartX=94 StartY=27.4 StartZ=0 EndX=96 EndY=27.4 EndZ=0
    g15: LineSegment StartX=96 StartY=27.4 StartZ=0 EndX=96 EndY=17.4 EndZ=0
    g16: ArcOfCircle CenterX=20 CenterY=26.9 CenterZ=0 NormalX=0 NormalY=0 NormalZ=1 AngleXU=0 Radius=0.5 StartAngle=0 EndAngle=1.5708
    g17: ArcOfCircle CenterX=20 CenterY=17.9 CenterZ=0 NormalX=0 NormalY=0 NormalZ=1 AngleXU=0 Radius=0.5 StartAngle=4.71239 EndAngle=6.28319
    g18: ArcOfCircle CenterX=20 CenterY=52.5 CenterZ=0 NormalX=0 NormalY=0 NormalZ=1 AngleXU=0 Radius=0.5 StartAngle=2.5e-15 EndAngle=1.5708
    g19: ArcOfCircle CenterX=20 CenterY=43.5 CenterZ=0 NormalX=0 NormalY=0 NormalZ=1 AngleXU=0 Radius=0.5 StartAngle=4.71239 EndAngle=6.28319
    g20: ArcOfCircle CenterX=94 CenterY=52.5 CenterZ=0 NormalX=0 NormalY=0 NormalZ=1 AngleXU=0 Radius=0.5 StartAngle=1.5708 EndAngle=3.14159
    g21: ArcOfCircle CenterX=94 CenterY=43.5 CenterZ=0 NormalX=0 NormalY=0 NormalZ=1 AngleXU=0 Radius=0.5 StartAngle=3.14159 EndAngle=4.71239
    g22: ArcOfCircle CenterX=94 CenterY=26.9 CenterZ=0 NormalX=0 NormalY=0 NormalZ=1 AngleXU=0 Radius=0.5 StartAngle=1.5708 EndAngle=3.14159
    g23: ArcOfCircle CenterX=94 CenterY=17.9 CenterZ=0 NormalX=0 NormalY=0 NormalZ=1 AngleXU=0 Radius=0.5 StartAngle=3.14159 EndAngle=4.71239
  constraints (64):
    c: Coincident(g2,g3)
    c: Coincident(g3,g0)
    c: Horizontal(g0)
    c: Horizontal(g2)
    c: Vertical(g1)
    c: Vertical(g3)
    c: Coincident(g6,g7)
    c: Coincident(g7,g4)
    c: Horizontal(g4)
    c: Horizontal(g6)
    c: Vertical(g5)
    c: Vertical(g7)
    c: Coincident(g10,g11)
    c: Coincident(g11,g8)
    c: Horizontal(g8)
    c: Horizontal(g10)
    c: Vertical(g9)
    c: Vertical(g11)
    c: Coincident(g14,g15)
    c: Coincident(g15,g12)
    c: Horizontal(g12)
    c: Horizontal(g14)
    c: Vertical(g13)
    c: Vertical(g15)
    c: Equal(g10,g14)
    c: Equal(g5,g1)
    c: Equal(g1,g9)
    c: Equal(g9,g13)
    c: Horizontal(g1,g13)
    c: Vertical(g13,g9)
    c: DistanceY(g-1,g0) = 17.4
    c: DistanceY(g3,g3) = 10
    c: DistanceY(g2,g4) = 15.6
    c: DistanceX(g-1,g0) = 18
    c: Tangent(g2,g16) = -1.5708
    c: Tangent(g1,g16) = -1.5708
    c: Tangent(g0,g17) = -1.5708
    c: Tangent(g1,g17) = -1.5708
    c: Equal(g17,g16)
    c: Radius(g16) = 0.5
    c: DistanceX(g2,g1) = 2.5
    c: Tangent(g6,g18) = -1.5708
    c: Tangent(g5,g18) = -1.5708
    c: Tangent(g5,g19) = -1.5708
    c: Tangent(g4,g19) = -1.5708
    c: Equal(g16,g19)
    c: Equal(g19,g18)
    c: Tangent(g9,g20) = -1.5708
    c: Tangent(g8,g20) = -1.5708
    c: Tangent(g9,g21) = -1.5708
    c: Tangent(g10,g21) = -1.5708
    c: Equal(g21,g20)
    c: Equal(g20,g18)
    c: Tangent(g13,g22) = 1.5708
    c: Tangent(g14,g22) = 1.5708
    c: Tangent(g13,g23) = 1.5708
    c: Tangent(g12,g23) = 1.5708
    c: Equal(g23,g22)
    c: Equal(g22,g21)
    c: Equal(g4,g2)
    c: Vertical(g4,g2)
    c: Equal(g12,g0)
    c: DistanceX(g0,g12) = 74
    c: Horizontal(g10,g4)
FEATURE [Sketcher::SketchObject] Sketch2498
  MapMode = 5
  Placement = pos=(20,0,0) rot=(0.57735,0.57735,0.57735;2.0944rad)
  sketch-geometry (1):
    g0: Circle CenterX=33 CenterY=37 CenterZ=0 NormalX=0 NormalY=0 NormalZ=1 AngleXU=0 Radius=1.6
  constraints (3):
    c: DistanceX(g-1,g0) = 33
    c: DistanceY(g-1,g0) = 37
    c: Radius(g0) = 1.6
FEATURE [Sketcher::SketchObject] Sketch2500
  MapMode = 5
  Support = -> [XY_Plane1016]
  sketch-geometry (8):
    g0: ArcOfCircle CenterX=25 CenterY=25 CenterZ=0 NormalX=0 NormalY=0 NormalZ=1 AngleXU=0 Radius=25 StartAngle=3.14159 EndAngle=4.71239
    g1: ArcOfCircle CenterX=20 CenterY=54 CenterZ=0 NormalX=0 NormalY=0 NormalZ=1 AngleXU=0 Radius=20 StartAngle=1.5708 EndAngle=3.14159
    g2: ArcOfCircle CenterX=94 CenterY=54 CenterZ=0 NormalX=0 NormalY=0 NormalZ=1 AngleXU=0 Radius=20 StartAngle=0 EndAngle=1.5708
    g3: ArcOfCircle CenterX=89 CenterY=25 CenterZ=0 NormalX=0 NormalY=0 NormalZ=1 AngleXU=0 Radius=25 StartAngle=4.71239 EndAngle=6.28319
    g4: LineSegment StartX=0 StartY=54 StartZ=0 EndX=0 EndY=25 EndZ=0
    g5: LineSegment StartX=25 StartY=0 StartZ=0 EndX=89 EndY=0 EndZ=0
    g6: LineSegment StartX=114 StartY=25 StartZ=0 EndX=114 EndY=54 EndZ=0
    g7: LineSegment StartX=20 StartY=74 StartZ=0 EndX=94 EndY=74 EndZ=0
  constraints (21):
    c: Tangent(g1,g4) = -1.5708
    c: Tangent(g3,g6) = -1.5708
    c: Horizontal(g7)
    c: Vertical(g4)
    c: Vertical(g6)
    c: Horizontal(g5)
    c: Horizontal(g3,g0)
    c: Horizontal(g1,g2)
    c: Coincident(g0,g5)
    c: Vertical(g0,g0)
    c: Radius(g2) = 20
    c: Radius(g3) = 25
    c: PointOnObject(g0,g-1)
    c: Tangent(g4,g0) = -1.5708
    c: Tangent(g7,g1) = 1.5708
    c: Tangent(g7,g2) = 1.5708
    c: Tangent(g6,g2) = -1.5708
    c: Tangent(g5,g3) = -1.5708
    c: DistanceX(g1,g2) = 114
    c: DistanceY(g0,g1) = 74
    c: PointOnObject(g0,g-2)
FEATURE [Sketcher::SketchObject] Sketch2503
  MapMode = 5
  Placement = pos=(0,0,0) rot=(0.57735,0.57735,0.57735;2.0944rad)
  Support = -> [YZ_Plane1009]
  sketch-geometry (3):
    g0: LineSegment StartX=0 StartY=0 StartZ=0 EndX=0 EndY=30 EndZ=0
    g1: LineSegment StartX=0 StartY=30 StartZ=0 EndX=66 EndY=0 EndZ=0
    g2: LineSegment StartX=66 StartY=0 StartZ=0 EndX=0 EndY=0 EndZ=0
  constraints (9):
    c: Coincident(g-1,g0)
    c: PointOnObject(g0,g-2)
    c: Coincident(g0,g1)
    c: PointOnObject(g1,g-1)
    c: Coincident(g1,g2)
    c: DistanceY(g0,g0) = 30
    c: DistanceX(g2,g2) = 66
    c: Coincident(g2,g0)
    c: Angle(g0,g1) = 1.14417
FEATURE [PartDesign::Pad] Pad1089  label="Baseblock019"
  Length = 28.5
  Length2 = 100
  Profile = -> Sketch2483
  Reversed = true
  Type = 0
FEATURE [Sketcher::SketchObject] Sketch2486
  MapMode = 5
  Placement = pos=(18,0,0) rot=(0.57735,-0.57735,-0.57735;2.0944rad)
  Support = -> [Pad1089]
  sketch-geometry (6):
    g0: LineSegment StartX=-62 StartY=15.75 StartZ=0 EndX=-4 EndY=42.1137 EndZ=0
    g1: LineSegment StartX=-4 StartY=42.1137 StartZ=0 EndX=-4 EndY=15.75 EndZ=0
    g2: LineSegment StartX=-4 StartY=15.75 StartZ=0 EndX=-62 EndY=15.75 EndZ=0
    g3: LineSegment StartX=-62 StartY=17.8863 StartZ=0 EndX=-4 EndY=44.25 EndZ=0
    g4: LineSegment StartX=-4 StartY=44.25 StartZ=0 EndX=-62 EndY=44.25 EndZ=0
    g5: LineSegment StartX=-62 StartY=44.25 StartZ=0 EndX=-62 EndY=17.8863 EndZ=0
  constraints (18):
    c: Coincident(g0,g1)
    c: Vertical(g1)
    c: Coincident(g1,g2)
    c: Coincident(g2,g0)
    c: Horizontal(g2)
    c: Coincident(g3,g4)
    c: Horizontal(g4)
    c: Coincident(g4,g5)
    c: Coincident(g5,g3)
    c: Vertical(g5)
    c: Parallel(g0,g3)
    c: Vertical(g0,g3)
    c: Vertical(g3,g0)
    c: Angle(g2,g0) = 0.426628
    c: DistanceX(g4,g4) = 58
    c: DistanceY(g1,g3) = 28.5
    c: DistanceX(g1,g-1) = 4
    c: DistanceY(g-1,g1) = 15.75
FEATURE [PartDesign::Pocket] Pocket867  label="Tilt Baseplate"
  BaseFeature = -> Pad1089
  Length = 80
  Length2 = 100
  Profile = -> Sketch2486
  Type = 0
FEATURE [PartDesign::Pad] Pad1090  label="Extend Baseplate004"
  BaseFeature = -> Pocket867
  Length = 44
  Length2 = 100
  Profile = -> Sketch2485
  Type = 0
FEATURE [Sketcher::SketchObject] Sketch2481
  ExternalGeometry = -> [Pad1090]
  MapMode = 5
  Placement = pos=(93.5,0,0) rot=(0.57735,0.57735,0.57735;2.0944rad)
  Support = -> [Pad1090]
  sketch-geometry (4):
    g0: LineSegment StartX=6.5 StartY=43.1136 StartZ=0 EndX=59.5 EndY=19.0227 EndZ=0
    g1: LineSegment StartX=59.5 StartY=19.0227 StartZ=0 EndX=59.5 EndY=44 EndZ=0
    g2: LineSegment StartX=59.5 StartY=44 StartZ=0 EndX=6.5 EndY=44 EndZ=0
    g3: LineSegment StartX=6.5 StartY=44 StartZ=0 EndX=6.5 EndY=43.1136 EndZ=0
  constraints (10):
    c: Coincident(g0,g1)
    c: Vertical(g1)
    c: Coincident(g1,g2)
    c: Horizontal(g2)
    c: Coincident(g2,g3)
    c: Coincident(g3,g0)
    c: Parallel(g0,g-3)
    c: DistanceX(g2,g2) = 53
    c: Coincident(g2,g-4)
    c: Coincident(g0,g-4)
FEATURE [PartDesign::Pocket] Pocket876  label="Remove Baseplate"
  BaseFeature = -> Pad1090
  Length = 80
  Length2 = 100
  Profile = -> Sketch2481
  Type = 0
FEATURE [PartDesign::Plane] DatumPlane009  label="Plane along tilt"
  Length = 124.323
  MapMode = 7
  Placement = pos=(96,11,38.9319) rot=(1,0,0;1.14417rad)
  ResizeMode = 0
  Support = -> [Pocket876]
  Width = 97.5041
FEATURE [Sketcher::SketchObject] Sketch2478
  MapMode = 5
  Placement = pos=(96,11,38.9319) rot=(1,0,0;1.14417rad)
  Support = -> [DatumPlane009]
  sketch-geometry (6):
    g0: LineSegment StartX=-75.5 StartY=-10.4308 StartZ=0 EndX=-51.5 EndY=-4 EndZ=0
    g1: LineSegment StartX=-51.5 StartY=-4 StartZ=0 EndX=-26.5 EndY=-4 EndZ=0
    g2: LineSegment StartX=-26.5 StartY=-4 StartZ=0 EndX=-2.5 EndY=-10.4308 EndZ=0
    g3: LineSegment StartX=-2.5 StartY=-10.4308 StartZ=0 EndX=-2.5 EndY=-38 EndZ=0
    g4: LineSegment StartX=-2.5 StartY=-38 StartZ=0 EndX=-75.5 EndY=-38 EndZ=0
    g5: LineSegment StartX=-75.5 StartY=-38 StartZ=0 EndX=-75.5 EndY=-10.4308 EndZ=0
  constraints (18):
    c: Coincident(g0,g1)
    c: Horizontal(g1)
    c: Coincident(g1,g2)
    c: Coincident(g2,g3)
    c: Vertical(g3)
    c: Coincident(g3,g4)
    c: Horizontal(g4)
    c: Coincident(g4,g5)
    c: Coincident(g5,g0)
    c: Vertical(g5)
    c: DistanceX(g4,g4) = 73
    c: DistanceX(g2,g-1) = 2.5
    c: Equal(g2,g0)
    c: Angle(g5,g0) = 1.8326
    c: Equal(g5,g3)
    c: DistanceY(g3,g-1) = 38
    c: DistanceX(g1,g1) = 25
    c: DistanceY(g1,g-1) = 4
FEATURE [PartDesign::Pocket] Pocket868  label="Tilt Sensors"
  BaseFeature = -> Pocket876
  Length = 65
  Length2 = 100
  Profile = -> Sketch2478
  Type = 4
FEATURE [Sketcher::SketchObject] Sketch2480
  ExternalGeometry = -> [Pocket868]
  MapMode = 5
  Placement = pos=(-6.01759,9.29318,20.445) rot=(0.991049,0.028262,0.130474;2.71867rad)
  Support = -> [Pocket868]
  sketch-geometry (8):
    g0: LineSegment [constr] StartX=52.2997 StartY=9.221 StartZ=0 EndX=52.2997 EndY=-19.8882 EndZ=0
    g1: LineSegment [constr] StartX=52.2997 StartY=-19.8882 StartZ=0 EndX=52.2997 EndY=-48.9973 EndZ=0
    g2: Circle CenterX=39.8763 CenterY=-8.34971 CenterZ=0 NormalX=0 NormalY=0 NormalZ=1 AngleXU=0 Radius=8.25
    g3: Circle CenterX=39.8763 CenterY=-34.3497 CenterZ=0 NormalX=0 NormalY=0 NormalZ=1 AngleXU=0 Radius=8.25
    g4: LineSegment [constr] StartX=39.8763 StartY=-8.34971 StartZ=0 EndX=39.8763 EndY=-21.3497 EndZ=0
    g5: LineSegment [constr] StartX=39.8763 StartY=-21.3497 StartZ=0 EndX=39.8763 EndY=-34.3497 EndZ=0
    g6: LineSegment [constr] StartX=52.2997 StartY=-19.8882 StartZ=0 EndX=39.8763 EndY=-21.3497 EndZ=0
    g7: LineSegment [constr] StartX=39.8763 StartY=-21.3497 StartZ=0 EndX=27.453 EndY=-22.8113 EndZ=0
  constraints (21):
    c: Coincident(g0,g-3)
    c: Vertical(g0)
    c: Coincident(g1,g-4)
    c: Equal(g1,g0)
    c: Radius(g2) = 8.25
    c: Equal(g3,g2)
    c: Coincident(g4,g2)
    c: Coincident(g5,g4)
    c: Coincident(g5,g3)
    c: Vertical(g5)
    c: Vertical(g4)
    c: Equal(g5,g4)
    c: DistanceY(g3,g2) = 26
    c: Coincident(g6,g0)
    c: Coincident(g6,g4)
    c: Coincident(g7,g4)
    c: Tangent(g7,g6)
    c: Parallel(g6,g-3)
    c: Equal(g6,g7)
    c: Coincident(g0,g1)
    c: PointOnObject(g7,g-5)
FEATURE [PartDesign::Pocket] Pocket866  label="Left Ultrasonic Sensor Holes"
  BaseFeature = -> Pocket868
  Length = 15
  Length2 = 100
  Profile = -> Sketch2480
  Type = 0
FEATURE [Sketcher::SketchObject] Sketch2488
  ExternalGeometry = -> [Pocket866]
  MapMode = 5
  Placement = pos=(13.6541,21.0866,46.3904) rot=(0.991049,-0.028262,-0.130474;2.71867rad)
  Support = -> [Pocket866]
  sketch-geometry (8):
    g0: LineSegment [constr] StartX=57.8159 StartY=9.221 StartZ=0 EndX=57.8159 EndY=-19.8882 EndZ=0
    g1: LineSegment [constr] StartX=57.8159 StartY=-19.8882 StartZ=0 EndX=57.8159 EndY=-48.9973 EndZ=0
    g2: LineSegment [constr] StartX=57.8159 StartY=-19.8882 StartZ=0 EndX=70.2392 EndY=-21.3497 EndZ=0
    g3: LineSegment [constr] StartX=70.2392 StartY=-21.3497 StartZ=0 EndX=82.6625 EndY=-22.8113 EndZ=0
    g4: LineSegment [constr] StartX=70.2392 StartY=-21.3497 StartZ=0 EndX=70.2392 EndY=-8.34971 EndZ=0
    g5: LineSegment [constr] StartX=70.2392 StartY=-21.3497 StartZ=0 EndX=70.2392 EndY=-34.3497 EndZ=0
    g6: Circle CenterX=70.2392 CenterY=-8.34971 CenterZ=0 NormalX=0 NormalY=0 NormalZ=1 AngleXU=0 Radius=8.25
    g7: Circle CenterX=70.2392 CenterY=-34.3497 CenterZ=0 NormalX=0 NormalY=0 NormalZ=1 AngleXU=0 Radius=8.25
  constraints (21):
    c: Coincident(g0,g-3)
    c: Vertical(g0)
    c: Coincident(g1,g0)
    c: Coincident(g1,g-4)
    c: Coincident(g2,g0)
    c: Coincident(g4,g2)
    c: Vertical(g4)
    c: Coincident(g5,g2)
    c: Vertical(g5)
    c: Tangent(g3,g2) = -1.5708
    c: Equal(g0,g1)
    c: Equal(g4,g5)
    c: Parallel(g3,g-3)
    c: Equal(g2,g3)
    c: Equal(g4,g5)
    c: PointOnObject(g3,g-5)
    c: Coincident(g6,g4)
    c: Coincident(g7,g5)
    c: Radius(g7) = 8.25
    c: Equal(g7,g6)
    c: DistanceY(g7,g6) = 26
FEATURE [PartDesign::Pad] Pad1092  label="Base"
  Length = 2
  Length2 = 100
  Profile = -> Sketch2466
  Type = 0
FEATURE [PartDesign::Pocket] Pocket878  label="Right Ultrasonic Sensor Holes"
  BaseFeature = -> Pocket866
  Length = 19
  Length2 = 100
  Profile = -> Sketch2488
  Type = 0
FEATURE [Sketcher::SketchObject] Sketch2484
  AttachmentOffset = pos=(0,0,-8) rot=(0,0,1;0rad)
  MapMode = 5
  Placement = pos=(-8.08814,12.4908,27.4797) rot=(0.991049,0.028262,0.130474;2.71867rad)
  Support = -> [Pocket878]
  sketch-geometry (4):
    g0: ArcOfCircle CenterX=32.5 CenterY=-25.25 CenterZ=0 NormalX=0 NormalY=0 NormalZ=1 AngleXU=0 Radius=2.25 StartAngle=3.14159 EndAngle=6.28319
    g1: ArcOfCircle CenterX=32.5 CenterY=-17.25 CenterZ=0 NormalX=0 NormalY=0 NormalZ=1 AngleXU=0 Radius=2.25 StartAngle=4e-16 EndAngle=3.14159
    g2: LineSegment StartX=34.75 StartY=-25.25 StartZ=0 EndX=34.75 EndY=-17.25 EndZ=0
    g3: LineSegment StartX=30.25 StartY=-25.25 StartZ=0 EndX=30.25 EndY=-17.25 EndZ=0
  constraints (10):
    c: Tangent(g0,g3) = 1.5708
    c: Tangent(g0,g2) = -1.5708
    c: Tangent(g2,g1) = -1.5708
    c: Tangent(g3,g1) = 1.5708
    c: Vertical(g2)
    c: Equal(g0,g1)
    c: Radius(g1) = 2.25
    c: DistanceY(g0,g1) = 8
    c: DistanceX(g-1,g1) = 32.5
    c: DistanceY(g1,g-1) = 17.25
FEATURE [PartDesign::Pocket] Pocket871  label="Left Ultrasonic Sensor Clock"
  BaseFeature = -> Pocket878
  Length = 14
  Length2 = 100
  Profile = -> Sketch2484
  Type = 0
FEATURE [Sketcher::SketchObject] Sketch2479
  AttachmentOffset = pos=(0,0,-8) rot=(0,0,1;0rad)
  MapMode = 5
  Placement = pos=(15.7247,24.2842,53.4252) rot=(0.991049,-0.028262,-0.130474;2.71867rad)
  Support = -> [Pocket871]
  sketch-geometry (4):
    g0: ArcOfCircle CenterX=77.5 CenterY=-25.25 CenterZ=0 NormalX=0 NormalY=0 NormalZ=1 AngleXU=0 Radius=2.25 StartAngle=3.14159 EndAngle=6.28319
    g1: ArcOfCircle CenterX=77.5 CenterY=-17.25 CenterZ=0 NormalX=0 NormalY=0 NormalZ=1 AngleXU=0 Radius=2.25 StartAngle=0 EndAngle=3.14159
    g2: LineSegment StartX=79.75 StartY=-25.25 StartZ=0 EndX=79.75 EndY=-17.25 EndZ=0
    g3: LineSegment StartX=75.25 StartY=-25.25 StartZ=0 EndX=75.25 EndY=-17.25 EndZ=0
  constraints (10):
    c: Tangent(g0,g3) = 1.5708
    c: Tangent(g0,g2) = -1.5708
    c: Tangent(g2,g1) = -1.5708
    c: Tangent(g3,g1) = 1.5708
    c: Vertical(g2)
    c: Equal(g0,g1)
    c: Radius(g1) = 2.25
    c: DistanceY(g0,g1) = 8
    c: DistanceY(g1,g-1) = 17.25
    c: DistanceX(g-1,g1) = 77.5
FEATURE [PartDesign::Pocket] Pocket879  label="Right Ultrasonic Sensor Clock"
  BaseFeature = -> Pocket871
  Length = 12
  Length2 = 100
  Profile = -> Sketch2479
  Type = 0
FEATURE [PartDesign::Pad] Pad1094  label="Baseplate047"
  Length = 82
  Length2 = 100
  Profile = -> Sketch2500
  Type = 0
FEATURE [PartDesign::Pocket] Pocket885  label="Camera and LED Holes"
  BaseFeature = -> Pocket879
  Length = 50
  Length2 = 100
  Profile = -> Sketch2487
  Reversed = true
  Type = 0
FEATURE [PartDesign::Pocket] Pocket865  label="Middle LED extended Pockets"
  BaseFeature = -> Pocket885
  Length = 2
  Length2 = 100
  Profile = -> Sketch2489
  Type = 4
FEATURE [PartDesign::Pocket] Pocket882  label="Cutout Sensorplate Screwholes"
  BaseFeature = -> Pocket865
  Length = 40
  Length2 = 100
  Profile = -> Sketch2494
  Type = 0
FEATURE [PartDesign::Fillet] Fillet266  label="Smooth Cutout"
  Base = -> Pocket882 [Edge230,Edge208,Edge206,Edge78,Edge221,Edge201,Edge199,Edge32]
  BaseFeature = -> Pocket882
  Radius = 1
FEATURE [PartDesign::Body] Body712  label="Sensormount"
  Group = -> [Sketch2483,Pad1089,Sketch2486,Pocket867,Sketch2485,Pad1090,Sketch2481,Pocket876,DatumPlane009,Sketch2478,Pocket868,Sketch2480,Pocket866,Sketch2488,Pocket878,Sketch2484,Pocket871,Sketch2479,Pocket879,Sketch2487,Pocket885,Sketch2489,Pocket865,Sketch2494,Pocket882,Fillet266]
  Origin = -> Origin1010
  Placement = pos=(0,-14.4809,31.8638) rot=(1,0,0;0.426558rad)
  Tip = -> Fillet266
FEATURE [PartDesign::Pocket] Pocket888  label="Tilt Nose"
  BaseFeature = -> Pad1094
  Length = 114
  Length2 = 100
  Profile = -> Sketch2503
  Reversed = true
  Type = 0
FEATURE [Sketcher::SketchObject] Sketch2504
  MapMode = 5
  Placement = pos=(0,0,82) rot=(0,0,1;0rad)
  Support = -> [Pocket888]
  sketch-geometry (8):
    g0: LineSegment StartX=25 StartY=60 StartZ=0 EndX=89 EndY=60 EndZ=0
    g1: LineSegment StartX=94 StartY=55 StartZ=0 EndX=94 EndY=11 EndZ=0
    g2: LineSegment StartX=89 StartY=6 StartZ=0 EndX=25 EndY=6 EndZ=0
    g3: LineSegment StartX=20 StartY=11 StartZ=0 EndX=20 EndY=55 EndZ=0
    g4: ArcOfCircle CenterX=25 CenterY=55 CenterZ=0 NormalX=0 NormalY=0 NormalZ=1 AngleXU=0 Radius=5 StartAngle=1.5708 EndAngle=3.14159
    g5: ArcOfCircle CenterX=89 CenterY=55 CenterZ=0 NormalX=0 NormalY=0 NormalZ=1 AngleXU=0 Radius=5 StartAngle=0 EndAngle=1.5708
    g6: ArcOfCircle CenterX=89 CenterY=11 CenterZ=0 NormalX=0 NormalY=0 NormalZ=1 AngleXU=0 Radius=5 StartAngle=4.71239 EndAngle=6.28319
    g7: ArcOfCircle CenterX=25 CenterY=11 CenterZ=0 NormalX=0 NormalY=0 NormalZ=1 AngleXU=0 Radius=5 StartAngle=3.14159 EndAngle=4.71239
  constraints (20):
    c: Horizontal(g0)
    c: Horizontal(g2)
    c: Vertical(g1)
    c: Vertical(g3)
    c: Tangent(g3,g4) = 1.5708
    c: Tangent(g0,g4) = 1.5708
    c: Tangent(g0,g5) = 1.5708
    c: Tangent(g1,g5) = 1.5708
    c: Tangent(g1,g6) = 1.5708
    c: Tangent(g2,g6) = 1.5708
    c: Tangent(g2,g7) = 1.5708
    c: Tangent(g3,g7) = 1.5708
    c: Equal(g4,g7)
    c: Equal(g7,g5)
    c: Equal(g5,g6)
    c: Radius(g5) = 5
    c: DistanceX(g-1,g3) = 20
    c: DistanceY(g-1,g7) = 11
    c: DistanceX(g4,g5) = 64
    c: DistanceY(g6,g5) = 44
FEATURE [PartDesign::Pocket] Pocket886  label="Sensorhole"
  BaseFeature = -> Pocket888
  Length = 0
  Length2 = 100
  Profile = -> Sketch2504
  Type = 1
FEATURE [PartDesign::Plane] DatumPlane
  Length = 148.245
  MapMode = 7
  Placement = pos=(0,25,18.6364) rot=(1,0,0;1.14417rad)
  ResizeMode = 0
  Support = -> [Pocket886]
  Width = 142.758
FEATURE [Sketcher::SketchObject] Sketch2482
  MapMode = 5
  Placement = pos=(0,25,18.6364) rot=(1,0,0;1.14417rad)
  Support = -> [DatumPlane]
  sketch-geometry (6):
    g0: LineSegment StartX=0 StartY=0 StartZ=0 EndX=0 EndY=16 EndZ=0
    g1: LineSegment StartX=0 StartY=16 StartZ=0 EndX=16 EndY=0 EndZ=0
    g2: LineSegment StartX=16 StartY=0 StartZ=0 EndX=0 EndY=0 EndZ=0
    g3: LineSegment StartX=98 StartY=0 StartZ=0 EndX=114 EndY=0 EndZ=0
    g4: LineSegment StartX=114 StartY=0 StartZ=0 EndX=114 EndY=16 EndZ=0
    g5: LineSegment StartX=114 StartY=16 StartZ=0 EndX=98 EndY=0 EndZ=0
  constraints (18):
    c: PointOnObject(g0,g-2)
    c: Vertical(g0)
    c: Coincident(g0,g1)
    c: PointOnObject(g1,g-1)
    c: Coincident(g1,g2)
    c: Coincident(g2,g0)
    c: Horizontal(g2)
    c: Horizontal(g3)
    c: Coincident(g3,g4)
    c: Vertical(g4)
    c: Coincident(g4,g5)
    c: Equal(g0,g2)
    c: Equal(g4,g3)
    c: Coincident(g5,g3)
    c: PointOnObject(g3,g-1)
    c: Equal(g2,g3)
    c: DistanceX(g0,g3) = 114
    c: DistanceX(g2,g2) = 16
FEATURE [PartDesign::Pocket] Pocket877  label="Sideburns"
  BaseFeature = -> Pocket886
  Length = 100
  Length2 = 100
  Profile = -> Sketch2482
  Type = 4
FEATURE [PartDesign::Pocket] Pocket875  label="Tilt Head"
  BaseFeature = -> Pocket877
  Length = 110
  Length2 = 100
  Profile = -> Sketch2490
  Reversed = true
  Type = 0
FEATURE [Sketcher::SketchObject] Sketch2493
  MapMode = 5
  Placement = pos=(-4.4e-15,11.3014,24.863) rot=(1,0,0;2.71496rad)
  Support = -> [Pocket875]
  sketch-geometry (6):
    g0: ArcOfCircle CenterX=30 CenterY=-30.8 CenterZ=0 NormalX=0 NormalY=0 NormalZ=1 AngleXU=0 Radius=30 StartAngle=3.14159 EndAngle=4.71239
    g1: ArcOfCircle CenterX=84 CenterY=-30.8 CenterZ=0 NormalX=0 NormalY=0 NormalZ=1 AngleXU=0 Radius=30 StartAngle=4.71239 EndAngle=6.28319
    g2: LineSegment StartX=30 StartY=-60.8 StartZ=0 EndX=84 EndY=-60.8 EndZ=0
    g3: LineSegment StartX=114 StartY=-30.8 StartZ=0 EndX=114 EndY=-80.8 EndZ=0
    g4: LineSegment StartX=114 StartY=-80.8 StartZ=0 EndX=0 EndY=-80.8 EndZ=0
    g5: LineSegment StartX=0 StartY=-80.8 StartZ=0 EndX=0 EndY=-30.8 EndZ=0
  constraints (16):
    c: PointOnObject(g0,g-2)
    c: Horizontal(g2)
    c: Coincident(g3,g4)
    c: Horizontal(g4)
    c: Coincident(g4,g5)
    c: Tangent(g0,g5) = 1.5708
    c: PointOnObject(g4,g-2)
    c: Tangent(g1,g3) = 1.5708
    c: Vertical(g3)
    c: Tangent(g2,g0) = -1.5708
    c: Tangent(g2,g1) = -1.5708
    c: Equal(g0,g1)
    c: Radius(g1) = 30
    c: DistanceX(g4,g4) = 114
    c: DistanceY(g0,g-1) = 60.8
    c: DistanceY(g4,g0) = 20
FEATURE [PartDesign::Pocket] Pocket887  label="Round Tilt Head"
  BaseFeature = -> Pocket875
  Length = 50
  Length2 = 100
  Profile = -> Sketch2493
  Type = 0
FEATURE [PartDesign::Thickness] Thickness  label="Make Shell"
  Base = -> Pocket887 [Face5]
  BaseFeature = -> Pocket887
  Join = 0
  Mode = 0
  Reversed = true
  Value = 2
FEATURE [PartDesign::Pocket] Pocket869  label="Sensorhole Screwholes"
  BaseFeature = -> Thickness
  Length = 5
  Length2 = 83
  Profile = -> Sketch2498
  Type = 4
FEATURE [Sketcher::SketchObject] Sketch2499
  MapMode = 5
  Placement = pos=(0,74,0) rot=(0,0.707107,0.707107;3.14159rad)
  Support = -> [Pocket869]
  sketch-geometry (10):
    g0: LineSegment StartX=-114 StartY=82 StartZ=0 EndX=-82 EndY=82 EndZ=0
    g1: LineSegment StartX=-82 StartY=82 StartZ=0 EndX=-82 EndY=68.25 EndZ=0
    g2: LineSegment StartX=-92 StartY=58.25 StartZ=0 EndX=-114 EndY=58.25 EndZ=0
    g3: LineSegment StartX=-114 StartY=58.25 StartZ=0 EndX=-114 EndY=82 EndZ=0
    g4: LineSegment StartX=0 StartY=82 StartZ=0 EndX=-32 EndY=82 EndZ=0
    g5: LineSegment StartX=-32 StartY=82 StartZ=0 EndX=-32 EndY=68.25 EndZ=0
    g6: LineSegment StartX=-22 StartY=58.25 StartZ=0 EndX=0 EndY=58.25 EndZ=0
    g7: LineSegment StartX=0 StartY=58.25 StartZ=0 EndX=0 EndY=82 EndZ=0
    g8: ArcOfCircle CenterX=-92 CenterY=68.25 CenterZ=0 NormalX=0 NormalY=0 NormalZ=1 AngleXU=0 Radius=10 StartAngle=4.71239 EndAngle=6.28319
    g9: ArcOfCircle CenterX=-22 CenterY=68.25 CenterZ=0 NormalX=0 NormalY=0 NormalZ=1 AngleXU=0 Radius=10 StartAngle=3.14159 EndAngle=4.71239
  constraints (28):
    c: Coincident(g0,g1)
    c: Coincident(g2,g3)
    c: Coincident(g3,g0)
    c: Horizontal(g0)
    c: Horizontal(g2)
    c: Vertical(g1)
    c: Vertical(g3)
    c: Coincident(g4,g5)
    c: Coincident(g6,g7)
    c: Coincident(g7,g4)
    c: Horizontal(g4)
    c: Horizontal(g6)
    c: Vertical(g5)
    c: Vertical(g7)
    c: PointOnObject(g4,g-2)
    c: Tangent(g2,g8) = 1.5708
    c: Tangent(g1,g8) = 1.5708
    c: Tangent(g5,g9) = -1.5708
    c: Tangent(g6,g9) = -1.5708
    c: Equal(g9,g8)
    c: Radius(g8) = 10
    c: Horizontal(g0,g4)
    c: Equal(g0,g4)
    c: Equal(g3,g7)
    c: DistanceX(g0,g4) = 50
    c: DistanceX(g0,g4) = 114
    c: DistanceY(g3,g3) = 23.75
    c: DistanceY(g-1,g4) = 82
FEATURE [PartDesign::Pocket] Pocket874
  BaseFeature = -> Pocket869
  Length = 40
  Length2 = 100
  Profile = -> Pocket869 [Face38]
  Type = 0
FEATURE [PartDesign::Pocket] Pocket872  label="Top Removal"
  BaseFeature = -> Pocket874
  Length = 40
  Length2 = 100
  Profile = -> Sketch2499
  Type = 0
FEATURE [Sketcher::SketchObject] Sketch2495
  MapMode = 5
  Placement = pos=(0,0,0) rot=(1,0,0;1.5708rad)
  Support = -> [Pocket872]
  sketch-geometry (10):
    g0: LineSegment StartX=0 StartY=82 StartZ=0 EndX=42 EndY=82 EndZ=0
    g1: LineSegment StartX=42 StartY=82 StartZ=0 EndX=42 EndY=68.25 EndZ=0
    g2: LineSegment StartX=32 StartY=58.25 StartZ=0 EndX=0 EndY=58.25 EndZ=0
    g3: LineSegment StartX=0 StartY=58.25 StartZ=0 EndX=0 EndY=82 EndZ=0
    g4: LineSegment StartX=114 StartY=82 StartZ=0 EndX=72 EndY=82 EndZ=0
    g5: LineSegment StartX=72 StartY=82 StartZ=0 EndX=72 EndY=68.25 EndZ=0
    g6: LineSegment StartX=82 StartY=58.25 StartZ=0 EndX=114 EndY=58.25 EndZ=0
    g7: LineSegment StartX=114 StartY=58.25 StartZ=0 EndX=114 EndY=82 EndZ=0
    g8: ArcOfCircle CenterX=32 CenterY=68.25 CenterZ=0 NormalX=0 NormalY=0 NormalZ=1 AngleXU=0 Radius=10 StartAngle=4.71239 EndAngle=6.28319
    g9: ArcOfCircle CenterX=82 CenterY=68.25 CenterZ=0 NormalX=0 NormalY=0 NormalZ=1 AngleXU=0 Radius=10 StartAngle=3.14159 EndAngle=4.71239
  constraints (28):
    c: Coincident(g0,g1)
    c: Coincident(g2,g3)
    c: Coincident(g3,g0)
    c: Horizontal(g0)
    c: Horizontal(g2)
    c: Vertical(g1)
    c: Vertical(g3)
    c: PointOnObject(g0,g-2)
    c: Coincident(g4,g5)
    c: Coincident(g6,g7)
    c: Coincident(g7,g4)
    c: Horizontal(g4)
    c: Horizontal(g6)
    c: Vertical(g5)
    c: Vertical(g7)
    c: Tangent(g2,g8) = 1.5708
    c: Tangent(g1,g8) = 1.5708
    c: Tangent(g5,g9) = -1.5708
    c: Tangent(g6,g9) = -1.5708
    c: Radius(g8) = 10
    c: Equal(g8,g9)
    c: Equal(g0,g4)
    c: Equal(g3,g7)
    c: Horizontal(g0,g4)
    c: DistanceX(g0,g4) = 30
    c: DistanceX(g0,g4) = 114
    c: DistanceY(g3,g3) = 23.75
    c: DistanceY(g-1,g0) = 82
FEATURE [PartDesign::Pocket] Pocket870  label="Bottom Removal"
  BaseFeature = -> Pocket872
  Length = 40
  Length2 = 100
  Profile = -> Sketch2495
  Type = 0
FEATURE [PartDesign::Fillet] Fillet267  label="Round Corners"
  Base = -> Pocket870 [Edge83,Edge84,Edge147,Edge146]
  BaseFeature = -> Pocket870
  Radius = 5
FEATURE [Sketcher::SketchObject] Sketch2502
  MapMode = 5
  Placement = pos=(0,74,0) rot=(0,0.707107,0.707107;3.14159rad)
  Support = -> [Fillet267]
  sketch-geometry (2):
    g0: Circle CenterX=-72 CenterY=77 CenterZ=0 NormalX=0 NormalY=0 NormalZ=1 AngleXU=0 Radius=1.6
    g1: Circle CenterX=-42 CenterY=77 CenterZ=0 NormalX=0 NormalY=0 NormalZ=1 AngleXU=0 Radius=1.6
  constraints (6):
    c: Equal(g1,g0)
    c: Horizontal(g0,g1)
    c: Radius(g1) = 1.6
    c: DistanceX(g0,g1) = 30
    c: DistanceX(g1,g-1) = 42
    c: DistanceY(g-1,g1) = 77
FEATURE [PartDesign::Pocket] Pocket884  label="Screwholes Top"
  BaseFeature = -> Fillet267
  Length = 5
  Length2 = 100
  Profile = -> Sketch2502
  Type = 0
FEATURE [Sketcher::SketchObject] Sketch2491
  MapMode = 5
  Placement = pos=(0,0,0) rot=(1,0,0;1.5708rad)
  Support = -> [Pocket884]
  sketch-geometry (2):
    g0: Circle CenterX=52 CenterY=77 CenterZ=0 NormalX=0 NormalY=0 NormalZ=1 AngleXU=0 Radius=1.6
    g1: Circle CenterX=62 CenterY=77 CenterZ=0 NormalX=0 NormalY=0 NormalZ=1 AngleXU=0 Radius=1.6
  constraints (6):
    c: Equal(g1,g0)
    c: Radius(g1) = 1.6
    c: Horizontal(g0,g1)
    c: DistanceX(g0,g1) = 10
    c: DistanceY(g-1,g1) = 77
    c: DistanceX(g-1,g0) = 52
FEATURE [PartDesign::Pocket] Pocket873  label="Screwholes Bottom"
  BaseFeature = -> Pocket884
  Length = 5
  Length2 = 100
  Profile = -> Sketch2491
  Type = 0
FEATURE [Sketcher::SketchObject] Sketch2501
  ExternalGeometry = -> [Pocket873]
  MapMode = 5
  Placement = pos=(18,0,0) rot=(0.57735,-0.57735,-0.57735;2.0944rad)
  Support = -> [Pocket873]
  sketch-geometry (3):
    g0: LineSegment StartX=-4 StartY=42 StartZ=0 EndX=-62 EndY=15.6364 EndZ=0
    g1: LineSegment StartX=-62 StartY=15.6364 StartZ=0 EndX=-62 EndY=42 EndZ=0
    g2: LineSegment StartX=-62 StartY=42 StartZ=0 EndX=-4 EndY=42 EndZ=0
  constraints (9):
    c: Coincident(g0,g1)
    c: Vertical(g1)
    c: Coincident(g1,g2)
    c: Coincident(g2,g0)
    c: Horizontal(g2)
    c: Parallel(g0,g-3)
    c: DistanceX(g0,g-1) = 4
    c: DistanceX(g2,g2) = 58
    c: DistanceY(g-1,g0) = 42
FEATURE [PartDesign::Pocket] Pocket883  label="Shorten Sensorhole"
  BaseFeature = -> Pocket873
  Length = 78
  Length2 = 100
  Profile = -> Sketch2501
  Type = 0
FEATURE [PartDesign::Plane] DatumPlane012  label="Plane along Sensorhole"
  Length = 148.245
  MapMode = 7
  Placement = pos=(96,11,38.8182) rot=(1,0,0;1.14417rad)
  ResizeMode = 0
  Support = -> [Pocket883]
  Width = 142.758
FEATURE [Sketcher::SketchObject] Sketch135
  AttachmentOffset = pos=(0,0,-8) rot=(0,0,1;0rad)
  MapMode = 5
  Placement = pos=(96,18.2829,35.5078) rot=(1,0,0;1.14417rad)
  Support = -> [DatumPlane012]
  sketch-geometry (8):
    g0: LineSegment StartX=-2 StartY=2 StartZ=0 EndX=14 EndY=2 EndZ=0
    g1: LineSegment StartX=14 StartY=2 StartZ=0 EndX=1 EndY=-11 EndZ=0
    g2: LineSegment StartX=1 StartY=-11 StartZ=0 EndX=-2 EndY=-11 EndZ=0
    g3: LineSegment StartX=-2 StartY=-11 StartZ=0 EndX=-2 EndY=2 EndZ=0
    g4: LineSegment StartX=-76 StartY=-11 StartZ=0 EndX=-76 EndY=2 EndZ=0
    g5: LineSegment StartX=-76 StartY=2 StartZ=0 EndX=-92 EndY=2 EndZ=0
    g6: LineSegment StartX=-92 StartY=2 StartZ=0 EndX=-79 EndY=-11 EndZ=0
    g7: LineSegment StartX=-79 StartY=-11 StartZ=0 EndX=-76 EndY=-11 EndZ=0
  constraints (24):
    c: Horizontal(g0)
    c: Coincident(g0,g1)
    c: Coincident(g1,g2)
    c: Horizontal(g2)
    c: Coincident(g2,g3)
    c: Vertical(g3)
    c: Angle(g1,g2) = 2.35619
    c: Vertical(g4)
    c: Coincident(g4,g5)
    c: Horizontal(g5)
    c: Coincident(g5,g6)
    c: Coincident(g6,g7)
    c: Horizontal(g7)
    c: Equal(g0,g5)
    c: Angle(g7,g6) = 2.35619
    c: Coincident(g0,g3)
    c: DistanceY(g-1,g0) = 2
    c: DistanceX(g0,g-1) = 2
    c: DistanceY(g2,g-1) = 11
    c: DistanceX(g0,g0) = 16
    c: Coincident(g7,g4)
    c: Horizontal(g4,g0)
    c: Horizontal(g4,g2)
    c: DistanceX(g4,g0) = 74
FEATURE [Sketcher::SketchObject] Sketch2496
  AttachmentOffset = pos=(0,0,-44) rot=(0,0,1;0rad)
  MapMode = 5
  Placement = pos=(96,51.0561,20.6109) rot=(1,0,0;1.14417rad)
  Support = -> [DatumPlane012]
  sketch-geometry (8):
    g0: LineSegment StartX=-2 StartY=2 StartZ=0 EndX=14 EndY=2 EndZ=0
    g1: LineSegment StartX=14 StartY=2 StartZ=0 EndX=1 EndY=-11 EndZ=0
    g2: LineSegment StartX=1 StartY=-11 StartZ=0 EndX=-2 EndY=-11 EndZ=0
    g3: LineSegment StartX=-2 StartY=-11 StartZ=0 EndX=-2 EndY=2 EndZ=0
    g4: LineSegment StartX=-76 StartY=-11 StartZ=0 EndX=-76 EndY=2 EndZ=0
    g5: LineSegment StartX=-76 StartY=2 StartZ=0 EndX=-92 EndY=2 EndZ=0
    g6: LineSegment StartX=-92 StartY=2 StartZ=0 EndX=-79 EndY=-11 EndZ=0
    g7: LineSegment StartX=-79 StartY=-11 StartZ=0 EndX=-76 EndY=-11 EndZ=0
  constraints (24):
    c: Horizontal(g0)
    c: Coincident(g0,g1)
    c: Coincident(g1,g2)
    c: Horizontal(g2)
    c: Coincident(g2,g3)
    c: Vertical(g3)
    c: Angle(g1,g2) = 2.35619
    c: Vertical(g4)
    c: Coincident(g4,g5)
    c: Horizontal(g5)
    c: Coincident(g5,g6)
    c: Coincident(g6,g7)
    c: Horizontal(g7)
    c: Equal(g0,g5)
    c: Angle(g7,g6) = 2.35619
    c: Coincident(g0,g3)
    c: DistanceY(g-1,g0) = 2
    c: DistanceX(g0,g-1) = 2
    c: DistanceY(g2,g-1) = 11
    c: DistanceX(g0,g0) = 16
    c: Coincident(g7,g4)
    c: Horizontal(g4,g0)
    c: Horizontal(g4,g2)
    c: DistanceX(g4,g0) = 74
FEATURE [PartDesign::Pad] Pad1091  label="Sensor Screwplate Bottom"
  BaseFeature = -> Pocket883
  Length = 8
  Length2 = 100
  Profile = -> Sketch135
  Reversed = true
  Type = 0
FEATURE [PartDesign::Pad] Pad1093  label="Sensor Screwplate Top"
  BaseFeature = -> Pad1091
  Length = 8
  Length2 = 100
  Profile = -> Sketch2496
  Type = 0
FEATURE [Sketcher::SketchObject] Sketch2492
  ExternalGeometry = -> [Pad1093]
  MapMode = 5
  Placement = pos=(0,17.3345,38.1358) rot=(-1,0,0;0.426627rad)
  Support = -> [Pad1093]
  sketch-geometry (4):
    g0: Circle CenterX=14 CenterY=33.951 CenterZ=0 NormalX=0 NormalY=0 NormalZ=1 AngleXU=0 Radius=1.6
    g1: Circle CenterX=14 CenterY=5.95095 CenterZ=0 NormalX=0 NormalY=0 NormalZ=1 AngleXU=0 Radius=1.6
    g2: Circle CenterX=100 CenterY=5.95095 CenterZ=0 NormalX=0 NormalY=0 NormalZ=1 AngleXU=0 Radius=1.6
    g3: Circle CenterX=100 CenterY=33.951 CenterZ=0 NormalX=0 NormalY=0 NormalZ=1 AngleXU=0 Radius=1.6
  constraints (12):
    c: Horizontal(g3,g0)
    c: Horizontal(g1,g2)
    c: Vertical(g2,g3)
    c: Vertical(g0,g1)
    c: Radius(g1) = 1.6
    c: Equal(g1,g0)
    c: Equal(g1,g3)
    c: Equal(g1,g2)
    c: DistanceX(g0,g3) = 86
    c: DistanceX(g-1,g0) = 14
    c: DistanceY(g1,g-3) = 4
    c: DistanceY(g1,g0) = 28
FEATURE [PartDesign::Pocket] Pocket880  label="Sensor Screwholes"
  BaseFeature = -> Pad1093
  Length = 7
  Length2 = 100
  Profile = -> Sketch2492
  Type = 0
FEATURE [Sketcher::SketchObject] Sketch2497
  ExternalGeometry = -> [Pocket880]
  MapMode = 5
  Placement = pos=(0,1.77608,-0.80731) rot=(1,0,0;1.14417rad)
  Support = -> [Pocket880]
  sketch-geometry (8):
    g0: LineSegment StartX=11 StartY=36.8906 StartZ=0 EndX=17 EndY=36.8906 EndZ=0
    g1: LineSegment StartX=17 StartY=36.8906 StartZ=0 EndX=17 EndY=39.8906 EndZ=0
    g2: LineSegment StartX=17 StartY=39.8906 StartZ=0 EndX=11 EndY=39.8906 EndZ=0
    g3: LineSegment StartX=11 StartY=39.8906 StartZ=0 EndX=11 EndY=36.8906 EndZ=0
    g4: LineSegment StartX=97 StartY=36.8906 StartZ=0 EndX=103 EndY=36.8906 EndZ=0
    g5: LineSegment StartX=103 StartY=36.8906 StartZ=0 EndX=103 EndY=39.8906 EndZ=0
    g6: LineSegment StartX=103 StartY=39.8906 StartZ=0 EndX=97 EndY=39.8906 EndZ=0
    g7: LineSegment StartX=97 StartY=39.8906 StartZ=0 EndX=97 EndY=36.8906 EndZ=0
  constraints (24):
    c: Coincident(g0,g1)
    c: Coincident(g1,g2)
    c: Coincident(g2,g3)
    c: Coincident(g3,g0)
    c: Horizontal(g0)
    c: Horizontal(g2)
    c: Vertical(g1)
    c: Vertical(g3)
    c: Coincident(g4,g5)
    c: Coincident(g5,g6)
    c: Coincident(g6,g7)
    c: Coincident(g7,g4)
    c: Horizontal(g4)
    c: Horizontal(g6)
    c: Vertical(g5)
    c: Vertical(g7)
    c: Horizontal(g1,g-3)
    c: Horizontal(g-3,g6)
    c: DistanceX(g6,g6) = 6
    c: DistanceY(g5,g5) = 3
    c: Equal(g1,g7)
    c: Equal(g2,g6)
    c: DistanceX(g1,g6) = 80
    c: DistanceX(g-1,g1) = 17
FEATURE [PartDesign::Pocket] Pocket881  label="Sensor Nutholes"
  BaseFeature = -> Pocket880
  Length = 40
  Length2 = 100
  Profile = -> Sketch2497
  Type = 0
FEATURE [PartDesign::Body] Body713  label="Front_Cover_Optimized"
  Group = -> [Sketch2500,Pad1094,Sketch2503,Pocket888,Sketch2504,Pocket886,DatumPlane,Sketch2482,Pocket877,Sketch2490,Pocket875,Sketch2493,Pocket887,Thickness,Sketch2498,Pocket869,Sketch2499,Pocket874,Pocket872,Sketch2495,Pocket870,Fillet267,Sketch2502,Pocket884,Sketch2491,Pocket873,Sketch2501,Pocket883,DatumPlane012,Sketch135,Pad1091,Sketch2496,Pad1093,Sketch2492,Pocket880,Sketch2497,Pocket881]
  Origin = -> Origin1011
  Placement = pos=(0,14.4624,-31.8173) rot=(1,0,0;0.426628rad)
  Tip = -> Pocket881
FEATURE [PartDesign::Pad] Pad1095  label="Camerawedge"
  BaseFeature = -> Pad1092
  Length = 18
  Length2 = 18
  Profile = -> Sketch2467
  Type = 4
FEATURE [Sketcher::SketchObject] Sketch2464
  MapMode = 5
  Placement = pos=(0,0,44) rot=(0,0,1;0rad)
  Support = -> [Pad1095]
  sketch-geometry (8):
    g0: LineSegment StartX=75 StartY=-2 StartZ=0 EndX=96 EndY=-2 EndZ=0
    g1: LineSegment StartX=96 StartY=-2 StartZ=0 EndX=96 EndY=44.5 EndZ=0
    g2: LineSegment StartX=96 StartY=44.5 StartZ=0 EndX=75 EndY=44.5 EndZ=0
    g3: LineSegment StartX=75 StartY=44.5 StartZ=0 EndX=75 EndY=-2 EndZ=0
    g4: LineSegment StartX=18 StartY=-2 StartZ=0 EndX=39 EndY=-2 EndZ=0
    g5: LineSegment StartX=39 StartY=-2 StartZ=0 EndX=39 EndY=44.5 EndZ=0
    g6: LineSegment StartX=39 StartY=44.5 StartZ=0 EndX=18 EndY=44.5 EndZ=0
    g7: LineSegment StartX=18 StartY=44.5 StartZ=0 EndX=18 EndY=-2 EndZ=0
  constraints (24):
    c: Coincident(g0,g1)
    c: Coincident(g1,g2)
    c: Coincident(g2,g3)
    c: Coincident(g3,g0)
    c: Horizontal(g0)
    c: Horizontal(g2)
    c: Vertical(g1)
    c: Vertical(g3)
    c: Coincident(g4,g5)
    c: Coincident(g5,g6)
    c: Coincident(g6,g7)
    c: Coincident(g7,g4)
    c: Horizontal(g4)
    c: Horizontal(g6)
    c: Vertical(g5)
    c: Vertical(g7)
    c: DistanceX(g6,g6) = 21
    c: DistanceX(g5,g2) = 36
    c: DistanceX(g-1,g5) = 39
    c: DistanceY(g7,g7) = 46.5
    c: Horizontal(g5,g2)
    c: Equal(g1,g7)
    c: Equal(g2,g6)
    c: DistanceY(g4,g-1) = 2
FEATURE [PartDesign::Pocket] Pocket061  label="Ultrasonic Sensor Holes"
  BaseFeature = -> Pad1095
  Length = 2
  Length2 = 100
  Profile = -> Sketch2464
  Type = 0
FEATURE [PartDesign::Fillet] Fillet265  label="Smooth Ultrasonic Sensor Holes"
  Base = -> Pocket061 [Edge58,Edge57,Edge55,Edge56,Edge50,Edge51,Edge52,Edge54]
  BaseFeature = -> Pocket061
  Radius = 1
FEATURE [Sketcher::SketchObject] Sketch2471
  ExternalGeometry = -> [Fillet265]
  MapMode = 5
  Placement = pos=(75,-1.65e-14,1.87e-14) rot=(0.57735,0.57735,0.57735;2.0944rad)
  Support = -> [Fillet265]
  sketch-geometry (9):
    g0: LineSegment StartX=-14.65 StartY=44 StartZ=0 EndX=1.35 EndY=44 EndZ=0
    g1: LineSegment StartX=1.35 StartY=44 StartZ=0 EndX=-1.38974 EndY=50.0274 EndZ=0
    g2: LineSegment StartX=-1.38974 StartY=50.0274 StartZ=0 EndX=-14.65 EndY=44 EndZ=0
    g3: LineSegment StartX=34.1145 StartY=66.1657 StartZ=0 EndX=37.425 EndY=58.8828 EndZ=0
    g4: LineSegment StartX=37.425 StartY=58.8828 StartZ=0 EndX=29.05 EndY=49 EndZ=0
    g5: LineSegment StartX=29.05 StartY=44 StartZ=0 EndX=49.05 EndY=44 EndZ=0
    g6: LineSegment StartX=49.05 StartY=44 StartZ=0 EndX=49.05 EndY=72.9546 EndZ=0
    g7: LineSegment StartX=49.05 StartY=72.9546 StartZ=0 EndX=34.1145 EndY=66.1657 EndZ=0
    g8: LineSegment StartX=29.05 StartY=44 StartZ=0 EndX=29.05 EndY=49 EndZ=0
  constraints (25):
    c: Horizontal(g0)
    c: Coincident(g0,g1)
    c: Coincident(g1,g2)
    c: Coincident(g0,g2)
    c: Coincident(g0,g-3)
    c: PointOnObject(g1,g-4)
    c: Perpendicular(g1,g2)
    c: DistanceX(g0,g0) = 16
    c: PointOnObject(g3,g-4)
    c: Coincident(g3,g4)
    c: Horizontal(g5)
    c: Coincident(g5,g6)
    c: Coincident(g6,g-4)
    c: Vertical(g6)
    c: Coincident(g6,g7)
    c: Coincident(g7,g3)
    c: Perpendicular(g7,g3)
    c: Horizontal(g5,g0)
    c: Distance(g3) = 8
    c: DistanceX(g5,g5) = 20
    c: Distance(g3,g1) = 39
    c: Coincident(g8,g5)
    c: Coincident(g8,g4)
    c: Vertical(g8)
    c: DistanceY(g8,g8) = 5
FEATURE [PartDesign::Pocket] Pocket062  label="Reduce Camerawedge"
  BaseFeature = -> Fillet265
  Length = 36
  Length2 = 100
  Profile = -> Sketch2471
  Type = 0
FEATURE [Sketcher::SketchObject] Sketch2474
  MapMode = 5
  Placement = pos=(-1.57e-14,-19.0839,41.9846) rot=(1,0,0;0.426628rad)
  Support = -> [Pocket062]
  sketch-geometry (15):
    g0: LineSegment [constr] StartX=66 StartY=48.5885 StartZ=0 EndX=48 EndY=48.5885 EndZ=0
    g1: LineSegment [constr] StartX=48 StartY=48.5885 StartZ=0 EndX=39 EndY=33 EndZ=0
    g2: LineSegment [constr] StartX=39 StartY=33 StartZ=0 EndX=48 EndY=17.4115 EndZ=0
    g3: LineSegment [constr] StartX=48 StartY=17.4115 StartZ=0 EndX=66 EndY=17.4115 EndZ=0
    g4: LineSegment [constr] StartX=66 StartY=17.4115 StartZ=0 EndX=75 EndY=33 EndZ=0
    g5: LineSegment [constr] StartX=75 StartY=33 StartZ=0 EndX=66 EndY=48.5885 EndZ=0
    g6: Circle [constr] CenterX=57 CenterY=33 CenterZ=0 NormalX=0 NormalY=0 NormalZ=1 AngleXU=0 Radius=18
    g7: Circle [constr] CenterX=66 CenterY=17.4115 CenterZ=0 NormalX=0 NormalY=0 NormalZ=1 AngleXU=0 Radius=1.6e-15
    g8: Circle [constr] CenterX=48 CenterY=48.5885 CenterZ=0 NormalX=0 NormalY=0 NormalZ=1 AngleXU=0 Radius=3.2
    g9: Circle [constr] CenterX=66 CenterY=48.5885 CenterZ=0 NormalX=0 NormalY=0 NormalZ=1 AngleXU=0 Radius=3.2
    g10: Circle CenterX=39 CenterY=33 CenterZ=0 NormalX=0 NormalY=0 NormalZ=1 AngleXU=0 Radius=3.2
    g11: Circle CenterX=48 CenterY=17.4115 CenterZ=0 NormalX=0 NormalY=0 NormalZ=1 AngleXU=0 Radius=3.2
    g12: Circle CenterX=66 CenterY=17.4115 CenterZ=0 NormalX=0 NormalY=0 NormalZ=1 AngleXU=0 Radius=3.2
    g13: Circle CenterX=75 CenterY=33 CenterZ=0 NormalX=0 NormalY=0 NormalZ=1 AngleXU=0 Radius=3.2
    g14: Circle CenterX=57 CenterY=33 CenterZ=0 NormalX=0 NormalY=0 NormalZ=1 AngleXU=0 Radius=7.5
  constraints (33):
    c: Coincident(g0,g1)
    c: Coincident(g1,g2)
    c: Coincident(g2,g3)
    c: Coincident(g3,g4)
    c: Coincident(g4,g5)
    c: Coincident(g5,g0)
    c: Equal(g0, g1-g5) x5
    c: PointOnObject(g0,g6)
    c: PointOnObject(g1,g6)
    c: PointOnObject(g2,g6)
    c: PointOnObject(g3,g6)
    c: PointOnObject(g4,g6)
    c: PointOnObject(g5,g6)
    c: DistanceX(g0,g0) = 18
    c: DistanceX(g-1,g6) = 57
    c: DistanceY(g-1,g6) = 33
    c: Horizontal(g0)
    c: Coincident(g7,g3)
    c: Tangent(g7,g6)
    c: Coincident(g8,g0)
    c: Coincident(g9,g0)
    c: Equal(g8,g9)
    c: Coincident(g10,g1)
    c: Coincident(g11,g2)
    c: Coincident(g12,g7)
    c: Coincident(g13,g4)
    c: Equal(g13,g10)
    c: Equal(g10,g11)
    c: Equal(g11,g12)
    c: Equal(g13,g9)
    c: Radius(g13) = 3.2
    c: Coincident(g14,g6)
    c: Radius(g14) = 7.5
FEATURE [Sketcher::SketchObject] Sketch148
  AttachmentOffset = pos=(0,0,-18) rot=(0,0,1;0rad)
  MapMode = 5
  Placement = pos=(-9.6e-15,-11.6355,25.598) rot=(1,0,0;0.426628rad)
  Support = -> [Pocket062]
  sketch-geometry (15):
    g0: LineSegment [constr] StartX=66 StartY=48.5885 StartZ=0 EndX=48 EndY=48.5885 EndZ=0
    g1: LineSegment [constr] StartX=48 StartY=48.5885 StartZ=0 EndX=39 EndY=33 EndZ=0
    g2: LineSegment [constr] StartX=39 StartY=33 StartZ=0 EndX=48 EndY=17.4115 EndZ=0
    g3: LineSegment [constr] StartX=48 StartY=17.4115 StartZ=0 EndX=66 EndY=17.4115 EndZ=0
    g4: LineSegment [constr] StartX=66 StartY=17.4115 StartZ=0 EndX=75 EndY=33 EndZ=0
    g5: LineSegment [constr] StartX=75 StartY=33 StartZ=0 EndX=66 EndY=48.5885 EndZ=0
    g6: Circle [constr] CenterX=57 CenterY=33 CenterZ=0 NormalX=0 NormalY=0 NormalZ=1 AngleXU=0 Radius=18
    g7: Circle [constr] CenterX=66 CenterY=17.4115 CenterZ=0 NormalX=0 NormalY=0 NormalZ=1 AngleXU=0 Radius=1.6e-15
    g8: Circle CenterX=48 CenterY=48.5885 CenterZ=0 NormalX=0 NormalY=0 NormalZ=1 AngleXU=0 Radius=3.2
    g9: Circle CenterX=66 CenterY=48.5885 CenterZ=0 NormalX=0 NormalY=0 NormalZ=1 AngleXU=0 Radius=3.2
    g10: Circle [constr] CenterX=39 CenterY=33 CenterZ=0 NormalX=0 NormalY=0 NormalZ=1 AngleXU=0 Radius=3.2
    g11: Circle [constr] CenterX=48 CenterY=17.4115 CenterZ=0 NormalX=0 NormalY=0 NormalZ=1 AngleXU=0 Radius=3.2
    g12: Circle [constr] CenterX=66 CenterY=17.4115 CenterZ=0 NormalX=0 NormalY=0 NormalZ=1 AngleXU=0 Radius=3.2
    g13: Circle [constr] CenterX=75 CenterY=33 CenterZ=0 NormalX=0 NormalY=0 NormalZ=1 AngleXU=0 Radius=3.2
    g14: Circle [constr] CenterX=57 CenterY=33 CenterZ=0 NormalX=0 NormalY=0 NormalZ=1 AngleXU=0 Radius=7.5
  constraints (33):
    c: Coincident(g0,g1)
    c: Coincident(g1,g2)
    c: Coincident(g2,g3)
    c: Coincident(g3,g4)
    c: Coincident(g4,g5)
    c: Coincident(g5,g0)
    c: Equal(g0, g1-g5) x5
    c: PointOnObject(g0,g6)
    c: PointOnObject(g1,g6)
    c: PointOnObject(g2,g6)
    c: PointOnObject(g3,g6)
    c: PointOnObject(g4,g6)
    c: PointOnObject(g5,g6)
    c: DistanceX(g0,g0) = 18
    c: DistanceX(g-1,g6) = 57
    c: DistanceY(g-1,g6) = 33
    c: Horizontal(g0)
    c: Coincident(g7,g3)
    c: Tangent(g7,g6)
    c: Coincident(g8,g0)
    c: Coincident(g9,g0)
    c: Equal(g8,g9)
    c: Coincident(g10,g1)
    c: Coincident(g11,g2)
    c: Coincident(g12,g7)
    c: Coincident(g13,g4)
    c: Equal(g13,g10)
    c: Equal(g10,g11)
    c: Equal(g11,g12)
    c: Equal(g13,g9)
    c: Radius(g13) = 3.2
    c: Coincident(g14,g6)
    c: Radius(g14) = 7.5
FEATURE [PartDesign::Pocket] Pocket063  label="Bottom LED and Camera Holes"
  BaseFeature = -> Pocket062
  Length = 40
  Length2 = 100
  Profile = -> Sketch2474
  Type = 0
FEATURE [PartDesign::Pocket] Pocket064  label="Top LED Holes"
  BaseFeature = -> Pocket063
  Length = 16
  Length2 = 100
  Profile = -> Sketch148
  Type = 0
FEATURE [Sketcher::SketchObject] Sketch149
  MapMode = 5
  Placement = pos=(-1.57e-14,-19.0839,41.9846) rot=(1,0,0;0.426628rad)
  Support = -> [Pocket064]
  sketch-geometry (5):
    g0: Circle [constr] CenterX=57 CenterY=33 CenterZ=0 NormalX=0 NormalY=0 NormalZ=1 AngleXU=0 Radius=1.6
    g1: Circle CenterX=42.75 CenterY=53 CenterZ=0 NormalX=0 NormalY=0 NormalZ=1 AngleXU=0 Radius=1.6
    g2: Circle CenterX=71.25 CenterY=53 CenterZ=0 NormalX=0 NormalY=0 NormalZ=1 AngleXU=0 Radius=1.6
    g3: Circle CenterX=71.25 CenterY=23.5 CenterZ=0 NormalX=0 NormalY=0 NormalZ=1 AngleXU=0 Radius=1.6
    g4: Circle CenterX=42.75 CenterY=23.5 CenterZ=0 NormalX=0 NormalY=0 NormalZ=1 AngleXU=0 Radius=1.6
  constraints (15):
    c: DistanceX(g-1,g0) = 57
    c: DistanceY(g-1,g0) = 33
    c: Horizontal(g4,g3)
    c: Horizontal(g1,g2)
    c: Vertical(g3,g2)
    c: Vertical(g4,g1)
    c: Equal(g1,g2)
    c: Equal(g2,g4)
    c: Equal(g4,g3)
    c: Radius(g2) = 1.6
    c: DistanceX(g1,g2) = 28.5
    c: DistanceY(g4,g1) = 29.5
    c: DistanceY(g3,g0) = 9.5
    c: Equal(g0,g3)
    c: DistanceX(g0,g3) = 14.25
FEATURE [PartDesign::Pocket] Pocket065  label="Camera Screwholes"
  BaseFeature = -> Pocket064
  Length = 8
  Length2 = 100
  Profile = -> Sketch149
  Type = 0
FEATURE [Sketcher::SketchObject] Sketch2469
  ExternalGeometry = -> [Pocket065]
  MapMode = 5
  Placement = pos=(75,-1.65e-14,1.87e-14) rot=(0.57735,0.57735,0.57735;2.0944rad)
  Support = -> [Pocket065]
  sketch-geometry (8):
    g0: LineSegment StartX=0.406178 StartY=48.6468 StartZ=0 EndX=5.86837 EndY=51.1296 EndZ=0
    g1: LineSegment StartX=5.86837 StartY=51.1296 StartZ=0 EndX=7.10979 EndY=48.3985 EndZ=0
    g2: LineSegment StartX=7.10979 StartY=48.3985 StartZ=0 EndX=1.64759 EndY=45.9157 EndZ=0
    g3: LineSegment StartX=1.64759 StartY=45.9157 StartZ=0 EndX=0.406178 EndY=48.6468 EndZ=0
    g4: LineSegment StartX=27.262 StartY=60.854 StartZ=0 EndX=32.7242 EndY=63.3368 EndZ=0
    g5: LineSegment StartX=32.7242 StartY=63.3368 StartZ=0 EndX=33.9656 EndY=60.6057 EndZ=0
    g6: LineSegment StartX=33.9656 StartY=60.6057 StartZ=0 EndX=28.5034 EndY=58.1229 EndZ=0
    g7: LineSegment StartX=28.5034 StartY=58.1229 StartZ=0 EndX=27.262 EndY=60.854 EndZ=0
  constraints (22):
    c: Coincident(g0,g1)
    c: Coincident(g1,g2)
    c: Coincident(g2,g3)
    c: Coincident(g3,g0)
    c: Coincident(g4,g5)
    c: Coincident(g5,g6)
    c: Coincident(g6,g7)
    c: Coincident(g7,g4)
    c: Parallel(g0,g2)
    c: Parallel(g4,g6)
    c: Parallel(g5,g7)
    c: Parallel(g7,g1)
    c: Parallel(g1,g3)
    c: Perpendicular(g5,g4)
    c: Distance(g5) = 3
    c: Distance(g4) = 6
    c: Distance(g4,g-3) = 2
    c: Symmetric(g4,g4,g-5)
    c: Symmetric(g0,g0,g-4)
    c: Distance(g0,g-3) = 2
    c: Equal(g1,g7)
    c: Equal(g2,g6)
FEATURE [Sketcher::SketchObject] Sketch2470
  AttachmentOffset = pos=(0,0,-36) rot=(0,0,1;0rad)
  ExternalGeometry = -> [Pocket065]
  MapMode = 5
  Placement = pos=(39,-8.5e-15,1.08e-14) rot=(0.57735,0.57735,0.57735;2.0944rad)
  Support = -> [Pocket065]
  sketch-geometry (8):
    g0: LineSegment StartX=0.406178 StartY=48.6468 StartZ=0 EndX=5.86837 EndY=51.1296 EndZ=0
    g1: LineSegment StartX=5.86837 StartY=51.1296 StartZ=0 EndX=7.10979 EndY=48.3985 EndZ=0
    g2: LineSegment StartX=7.10979 StartY=48.3985 StartZ=0 EndX=1.64759 EndY=45.9157 EndZ=0
    g3: LineSegment StartX=1.64759 StartY=45.9157 StartZ=0 EndX=0.406178 EndY=48.6468 EndZ=0
    g4: LineSegment StartX=27.262 StartY=60.854 StartZ=0 EndX=32.7242 EndY=63.3368 EndZ=0
    g5: LineSegment StartX=32.7242 StartY=63.3368 StartZ=0 EndX=33.9656 EndY=60.6057 EndZ=0
    g6: LineSegment StartX=33.9656 StartY=60.6057 StartZ=0 EndX=28.5034 EndY=58.1229 EndZ=0
    g7: LineSegment StartX=28.5034 StartY=58.1229 StartZ=0 EndX=27.262 EndY=60.854 EndZ=0
  constraints (22):
    c: Coincident(g0,g1)
    c: Coincident(g1,g2)
    c: Coincident(g2,g3)
    c: Coincident(g3,g0)
    c: Coincident(g4,g5)
    c: Coincident(g5,g6)
    c: Coincident(g6,g7)
    c: Coincident(g7,g4)
    c: Parallel(g0,g2)
    c: Parallel(g4,g6)
    c: Parallel(g5,g7)
    c: Parallel(g7,g1)
    c: Parallel(g1,g3)
    c: Perpendicular(g5,g4)
    c: Distance(g5) = 3
    c: Distance(g4) = 6
    c: Distance(g4,g-3) = 2
    c: Symmetric(g4,g4,g-5)
    c: Symmetric(g0,g0,g-4)
    c: Distance(g0,g-3) = 2
    c: Equal(g1,g7)
    c: Equal(g2,g6)
FEATURE [PartDesign::Pocket] Pocket066  label="Camera Nutholes Right"
  BaseFeature = -> Pocket065
  Length = 7
  Length2 = 100
  Profile = -> Sketch2469
  Type = 0
FEATURE [PartDesign::Pocket] Pocket067  label="Camera Nutholes Left"
  BaseFeature = -> Pocket066
  Length = 7
  Length2 = 100
  Profile = -> Sketch2470
  Reversed = true
  Type = 0
FEATURE [Sketcher::SketchObject] Sketch2472
  MapMode = 5
  Placement = pos=(-1.57e-14,-19.0839,41.9846) rot=(1,0,0;0.426628rad)
  Support = -> [Pocket067]
  sketch-geometry (20):
    g0: LineSegment StartX=48 StartY=42 StartZ=0 EndX=66 EndY=42 EndZ=0
    g1: LineSegment StartX=66 StartY=42 StartZ=0 EndX=66 EndY=35.5 EndZ=0
    g2: LineSegment StartX=66 StartY=35.5 StartZ=0 EndX=67 EndY=35.5 EndZ=0
    g3: ArcOfCircle CenterX=67 CenterY=33 CenterZ=0 NormalX=0 NormalY=0 NormalZ=1 AngleXU=0 Radius=2.5 StartAngle=4.71239 EndAngle=7.85398
    g4: LineSegment StartX=67 StartY=30.5 StartZ=0 EndX=66 EndY=30.5 EndZ=0
    g5: LineSegment StartX=66 StartY=30.5 StartZ=0 EndX=66 EndY=24 EndZ=0
    g6: LineSegment StartX=66 StartY=24 StartZ=0 EndX=59.5 EndY=24 EndZ=0
    g7: LineSegment StartX=59.5 StartY=24 StartZ=0 EndX=59.5 EndY=22 EndZ=0
    g8: LineSegment StartX=59.5 StartY=22 StartZ=0 EndX=54.5 EndY=22 EndZ=0
    g9: LineSegment StartX=54.5 StartY=22 StartZ=0 EndX=54.5 EndY=24 EndZ=0
    g10: LineSegment StartX=54.5 StartY=24 StartZ=0 EndX=48 EndY=24 EndZ=0
    g11: LineSegment StartX=48 StartY=24 StartZ=0 EndX=48 EndY=30.5 EndZ=0
    g12: LineSegment StartX=48 StartY=30.5 StartZ=0 EndX=47 EndY=30.5 EndZ=0
    g13: ArcOfCircle CenterX=47 CenterY=33 CenterZ=0 NormalX=0 NormalY=0 NormalZ=1 AngleXU=0 Radius=2.5 StartAngle=1.5708 EndAngle=4.71239
    g14: LineSegment StartX=47 StartY=35.5 StartZ=0 EndX=48 EndY=35.5 EndZ=0
    g15: LineSegment StartX=48 StartY=35.5 StartZ=0 EndX=48 EndY=42 EndZ=0
    g16: LineSegment [constr] StartX=48 StartY=42 StartZ=0 EndX=57 EndY=33 EndZ=0
    g17: LineSegment [constr] StartX=57 StartY=33 StartZ=0 EndX=66 EndY=42 EndZ=0
    g18: LineSegment [constr] StartX=57 StartY=33 StartZ=0 EndX=66 EndY=24 EndZ=0
    g19: LineSegment [constr] StartX=57 StartY=33 StartZ=0 EndX=48 EndY=24 EndZ=0
  constraints (55):
    c: Horizontal(g0)
    c: Coincident(g0,g1)
    c: Vertical(g1)
    c: Coincident(g1,g2)
    c: Tangent(g2,g3) = 1.5708
    c: Tangent(g3,g4) = 1.5708
    c: Coincident(g4,g5)
    c: Vertical(g5)
    c: Coincident(g5,g6)
    c: Horizontal(g6)
    c: Coincident(g6,g7)
    c: Coincident(g7,g8)
    c: Horizontal(g8)
    c: Coincident(g8,g9)
    c: Coincident(g9,g10)
    c: Horizontal(g10)
    c: Coincident(g10,g11)
    c: Coincident(g11,g12)
    c: Tangent(g12,g13) = 1.5708
    c: Tangent(g13,g14) = 1.5708
    c: Coincident(g14,g15)
    c: Vertical(g15)
    c: Coincident(g15,g0)
    c: Vertical(g11)
    c: Vertical(g9)
    c: Vertical(g7)
    c: Horizontal(g12)
    c: Horizontal(g14)
    c: Horizontal(g2)
    c: Horizontal(g4)
    c: Equal(g3,g13)
    c: Equal(g14,g2)
    c: Equal(g1,g15)
    c: Equal(g11,g5)
    c: Equal(g6,g10)
    c: DistanceX(g8,g8) = 5
    c: DistanceY(g7,g7) = 2
    c: Vertical(g11,g14)
    c: DistanceX(g13,g3) = 20
    c: Radius(g13) = 2.5
    c: DistanceX(g0,g0) = 18
    c: DistanceY(g5,g0) = 18
    c: Coincident(g16,g0)
    c: Coincident(g17,g16)
    c: Coincident(g17,g0)
    c: Coincident(g18,g5)
    c: Coincident(g19,g16)
    c: Coincident(g19,g10)
    c: Coincident(g18,g16)
    c: Equal(g17,g16)
    c: Equal(g16,g19)
    c: Equal(g19,g18)
    c: Horizontal(g13,g16)
    c: DistanceX(g-1,g16) = 57
    c: DistanceY(g-1,g16) = 33
FEATURE [PartDesign::Pocket] Pocket068  label="Camerasensor Pocket"
  BaseFeature = -> Pocket067
  Length = 9.5
  Length2 = 100
  Profile = -> Sketch2472
  Type = 0
FEATURE [Sketcher::SketchObject] Sketch2473
  MapMode = 5
  Placement = pos=(-1.57e-14,-19.0839,41.9846) rot=(1,0,0;0.426628rad)
  Support = -> [Pocket068]
  sketch-geometry (4):
    g0: LineSegment StartX=45 StartY=51 StartZ=0 EndX=69 EndY=51 EndZ=0
    g1: LineSegment StartX=69 StartY=51 StartZ=0 EndX=69 EndY=46 EndZ=0
    g2: LineSegment StartX=69 StartY=46 StartZ=0 EndX=45 EndY=46 EndZ=0
    g3: LineSegment StartX=45 StartY=46 StartZ=0 EndX=45 EndY=51 EndZ=0
  constraints (12):
    c: Coincident(g0,g1)
    c: Coincident(g1,g2)
    c: Coincident(g2,g3)
    c: Coincident(g3,g0)
    c: Horizontal(g0)
    c: Horizontal(g2)
    c: Vertical(g1)
    c: Vertical(g3)
    c: DistanceX(g0,g0) = 24
    c: DistanceY(g1,g1) = 5
    c: DistanceX(g-1,g2) = 45
    c: DistanceY(g-1,g2) = 46
FEATURE [PartDesign::Pocket] Pocket069  label="Camerapins Pocket"
  BaseFeature = -> Pocket068
  Length = 1.5
  Length2 = 100
  Profile = -> Sketch2473
  Type = 0
FEATURE [PartDesign::Pad] Pad1096  label="Ultrasonic Sensor Restrain"
  BaseFeature = -> Pocket069
  Length = 2
  Length2 = 100
  Profile = -> Sketch2475
  Type = 0
FEATURE [Sketcher::SketchObject] Sketch2476
  MapMode = 5
  Placement = pos=(-9.7e-15,0,44) rot=(0,0,1;0rad)
  Support = -> [Pad1096]
  sketch-geometry (18):
    g0: ArcOfCircle CenterX=44.5 CenterY=-3.5 CenterZ=0 NormalX=0 NormalY=0 NormalZ=1 AngleXU=0 Radius=1 StartAngle=1.5708 EndAngle=4.71239
    g1: ArcOfCircle CenterX=51.5 CenterY=-3.5 CenterZ=0 NormalX=0 NormalY=0 NormalZ=1 AngleXU=0 Radius=1 StartAngle=4.71239 EndAngle=7.85398
    g2: LineSegment StartX=44.5 StartY=-4.5 StartZ=0 EndX=51.5 EndY=-4.5 EndZ=0
    g3: LineSegment StartX=44.5 StartY=-2.5 StartZ=0 EndX=51.5 EndY=-2.5 EndZ=0
    g4: ArcOfCircle CenterX=44.5 CenterY=30.5 CenterZ=0 NormalX=0 NormalY=0 NormalZ=1 AngleXU=0 Radius=1 StartAngle=1.5708 EndAngle=4.71239
    g5: ArcOfCircle CenterX=51.5 CenterY=30.5 CenterZ=0 NormalX=0 NormalY=0 NormalZ=1 AngleXU=0 Radius=1 StartAngle=4.71239 EndAngle=7.85398
    g6: LineSegment StartX=44.5 StartY=29.5 StartZ=0 EndX=51.5 EndY=29.5 EndZ=0
    g7: LineSegment StartX=44.5 StartY=31.5 StartZ=0 EndX=51.5 EndY=31.5 EndZ=0
    g8: ArcOfCircle CenterX=62.5 CenterY=30.5 CenterZ=0 NormalX=0 NormalY=0 NormalZ=1 AngleXU=0 Radius=1 StartAngle=1.5708 EndAngle=4.71239
    g9: ArcOfCircle CenterX=69.5 CenterY=30.5 CenterZ=0 NormalX=0 NormalY=0 NormalZ=1 AngleXU=0 Radius=1 StartAngle=4.71239 EndAngle=7.85398
    g10: LineSegment StartX=62.5 StartY=29.5 StartZ=0 EndX=69.5 EndY=29.5 EndZ=0
    g11: LineSegment StartX=62.5 StartY=31.5 StartZ=0 EndX=69.5 EndY=31.5 EndZ=0
    g12: ArcOfCircle CenterX=62.5 CenterY=-3.5 CenterZ=0 NormalX=0 NormalY=0 NormalZ=1 AngleXU=0 Radius=1 StartAngle=1.5708 EndAngle=4.71239
    g13: ArcOfCircle CenterX=69.5 CenterY=-3.5 CenterZ=0 NormalX=0 NormalY=0 NormalZ=1 AngleXU=0 Radius=1 StartAngle=4.71239 EndAngle=7.85398
    g14: LineSegment StartX=62.5 StartY=-4.5 StartZ=0 EndX=69.5 EndY=-4.5 EndZ=0
    g15: LineSegment StartX=62.5 StartY=-2.5 StartZ=0 EndX=69.5 EndY=-2.5 EndZ=0
    g16: LineSegment [constr] StartX=57 StartY=40 StartZ=0 EndX=57 EndY=-30 EndZ=0
    g17: LineSegment [constr] StartX=48 StartY=40 StartZ=0 EndX=48 EndY=-30 EndZ=0
  constraints (45):
    c: Tangent(g0,g3) = 1.5708
    c: Tangent(g0,g2) = -1.5708
    c: Tangent(g2,g1) = -1.5708
    c: Tangent(g3,g1) = 1.5708
    c: Horizontal(g2)
    c: Equal(g0,g1)
    c: Tangent(g4,g7) = 1.5708
    c: Tangent(g4,g6) = -1.5708
    c: Tangent(g6,g5) = -1.5708
    c: Tangent(g7,g5) = 1.5708
    c: Horizontal(g6)
    c: Equal(g4,g5)
    c: Tangent(g8,g11) = 1.5708
    c: Tangent(g8,g10) = -1.5708
    c: Tangent(g10,g9) = -1.5708
    c: Tangent(g11,g9) = 1.5708
    c: Horizontal(g10)
    c: Equal(g8,g9)
    c: Tangent(g12,g15) = 1.5708
    c: Tangent(g12,g14) = -1.5708
    c: Tangent(g14,g13) = -1.5708
    c: Tangent(g15,g13) = 1.5708
    c: Horizontal(g14)
    c: Equal(g12,g13)
    c: Equal(g1,g12)
    c: Equal(g12,g5)
    c: Equal(g5,g8)
    c: Horizontal(g1,g12)
    c: Vertical(g4,g0)
    c: Equal(g11,g7)
    c: Equal(g7,g3)
    c: Equal(g3,g15)
    c: DistanceY(g0,g-1) = 2.5
    c: DistanceX(g-1,g16) = 57
    c: DistanceY(g16,g-1) = 30
    c: DistanceY(g-1,g16) = 40
    c: Symmetric(g1,g12,g16)
    c: Symmetric(g5,g8,g16)
    c: Radius(g13) = 1
    c: DistanceX(g17,g16) = 9
    c: Symmetric(g4,g5,g17)
    c: DistanceX(g3,g3) = 7
    c: Horizontal(g17,g16)
    c: Horizontal(g17,g16)
    c: DistanceY(g0,g4) = 32
FEATURE [PartDesign::Pad] Pad1097  label="Top and Bottom LED Restrain"
  BaseFeature = -> Pad1096
  Length = 1
  Length2 = 100
  Profile = -> Sketch2476
  Type = 0
FEATURE [Sketcher::SketchObject] Sketch2477
  AttachmentOffset = pos=(0,0,-11) rot=(0,0,1;0rad)
  ExternalGeometry = -> [Pad1097]
  MapMode = 5
  Placement = pos=(0,11,2.4e-15) rot=(1,0,0;1.5708rad)
  Support = -> [XZ_Plane1006]
  sketch-geometry (9):
    g0: LineSegment StartX=45.5 StartY=44 StartZ=0 EndX=40.5 EndY=44 EndZ=0
    g1: LineSegment StartX=40.5 StartY=44 StartZ=0 EndX=40.5 EndY=46 EndZ=0
    g2: LineSegment StartX=40.5 StartY=46 StartZ=0 EndX=45.5 EndY=46 EndZ=0
    g3: LineSegment StartX=45.5 StartY=46 StartZ=0 EndX=45.5 EndY=44 EndZ=0
    g4: LineSegment StartX=73.5 StartY=44 StartZ=0 EndX=68.5 EndY=44 EndZ=0
    g5: LineSegment StartX=68.5 StartY=44 StartZ=0 EndX=68.5 EndY=46 EndZ=0
    g6: LineSegment StartX=68.5 StartY=46 StartZ=0 EndX=73.5 EndY=46 EndZ=0
    g7: LineSegment StartX=73.5 StartY=46 StartZ=0 EndX=73.5 EndY=44 EndZ=0
    g8: LineSegment [constr] StartX=57 StartY=70 StartZ=0 EndX=57 EndY=0 EndZ=0
  constraints (26):
    c: Coincident(g0,g1)
    c: Coincident(g1,g2)
    c: Coincident(g2,g3)
    c: Coincident(g3,g0)
    c: Horizontal(g0)
    c: Horizontal(g2)
    c: Vertical(g1)
    c: Vertical(g3)
    c: Coincident(g4,g5)
    c: Coincident(g5,g6)
    c: Coincident(g6,g7)
    c: Coincident(g7,g4)
    c: Horizontal(g4)
    c: Horizontal(g6)
    c: Vertical(g5)
    c: Vertical(g7)
    c: Equal(g1,g7)
    c: DistanceY(g5,g5) = 2
    c: PointOnObject(g8,g-1)
    c: DistanceY(g8,g8) = 70
    c: Symmetric(g1,g6,g8)
    c: Symmetric(g5,g2,g8)
    c: DistanceX(g-1,g8) = 57
    c: Horizontal(g0,g-3)
    c: DistanceX(g2,g2) = 5
    c: DistanceX(g2,g5) = 23
FEATURE [PartDesign::Pad] Pad1098  label="Middle LED Restrain"
  BaseFeature = -> Pad1097
  Length = 15
  Length2 = 100
  Profile = -> Sketch2477
  Reversed = true
  Type = 0
FEATURE [Sketcher::SketchObject] Sketch2468
  MapMode = 5
  Placement = pos=(0,0,44) rot=(0,0,1;0rad)
  Support = -> [Pad1098]
  sketch-geometry (4):
    g0: Circle CenterX=14 CenterY=33.95 CenterZ=0 NormalX=0 NormalY=0 NormalZ=1 AngleXU=0 Radius=1.6
    g1: Circle CenterX=100 CenterY=33.95 CenterZ=0 NormalX=0 NormalY=0 NormalZ=1 AngleXU=0 Radius=1.6
    g2: Circle CenterX=100 CenterY=5.95 CenterZ=0 NormalX=0 NormalY=0 NormalZ=1 AngleXU=0 Radius=1.6
    g3: Circle CenterX=14 CenterY=5.95 CenterZ=0 NormalX=0 NormalY=0 NormalZ=1 AngleXU=0 Radius=1.6
  constraints (12):
    c: Equal(g0,g1)
    c: Equal(g1,g2)
    c: Equal(g2,g3)
    c: Horizontal(g3,g2)
    c: Horizontal(g1,g0)
    c: Vertical(g0,g3)
    c: Vertical(g2,g1)
    c: DistanceY(g2,g1) = 28
    c: DistanceX(g0,g1) = 86
    c: DistanceX(g-1,g3) = 14
    c: DistanceY(g-1,g3) = 5.95
    c: Radius(g3) = 1.6
FEATURE [PartDesign::Pocket] Pocket070  label="Mounting Screwholes"
  BaseFeature = -> Pad1098
  Length = 5
  Length2 = 100
  Profile = -> Sketch2468
  Type = 0
FEATURE [PartDesign::Body] Body714  label="Cameramount"
  Group = -> [Sketch2466,Pad1092,Sketch2467,Pad1095,Sketch2464,Pocket061,Fillet265,Sketch2471,Pocket062,Sketch2474,Pocket063,Sketch148,Pocket064,Sketch149,Pocket065,Sketch2469,Pocket066,Sketch2470,Pocket067,Sketch2472,Pocket068,Sketch2473,Pocket069,Sketch2475,Pad1096,Sketch2476,Pad1097,Sketch2477,Pad1098,Sketch2468,Pocket070]
  Origin = -> Origin1009
  Placement = pos=(0,-14.45,31.85) rot=(0,0,1;0rad)
  Tip = -> Pocket070
FEATURE [Sketcher::SketchObject] Sketch2505
  MapMode = 5
  Placement = pos=(0,0,0) rot=(1,0,0;1.5708rad)
  Support = -> [XZ_Plane1051]
  sketch-geometry (4):
    g0: LineSegment StartX=-0.32 StartY=-3 StartZ=0 EndX=0.32 EndY=-3 EndZ=0
    g1: LineSegment StartX=0.32 StartY=-3 StartZ=0 EndX=0.32 EndY=8.54 EndZ=0
    g2: LineSegment StartX=0.32 StartY=8.54 StartZ=0 EndX=-0.32 EndY=8.54 EndZ=0
    g3: LineSegment StartX=-0.32 StartY=8.54 StartZ=0 EndX=-0.32 EndY=-3 EndZ=0
  constraints (11):
    c: Coincident(g0,g1)
    c: Coincident(g1,g2)
    c: Coincident(g2,g3)
    c: Coincident(g3,g0)
    c: Horizontal(g0)
    c: Vertical(g1)
    c: Vertical(g3)
    c: DistanceY(g-1,g1) = 8.54
    c: DistanceY(g0,g-1) = 3
    c: Symmetric(g2,g1,g-2)
    c: DistanceX(g2,g2) = 0.64
FEATURE [PartDesign::Pad] Pad060
  Length = 2.5
  Length2 = 100
  Profile = -> Sketch205
  Type = 0
FEATURE [PartDesign::Chamfer] Chamfer558
  Base = -> Pad060 [Edge2,Edge1,Edge5,Edge8]
  BaseFeature = -> Pad060
  Size = 0.2
FEATURE [PartDesign::Chamfer] Chamfer561
  Base = -> Chamfer558 [Face5,Face2]
  BaseFeature = -> Chamfer558
  Size = 0.05
FEATURE [PartDesign::Pad] Pad061
  Length = 0.32
  Length2 = 0.32
  Placement = pos=(0,0,0) rot=(1,0,0;1.5708rad)
  Profile = -> Sketch206
  Type = 4
FEATURE [PartDesign::Chamfer] Chamfer559
  Base = -> Pad061 [Face3,Face1]
  BaseFeature = -> Pad061
  Placement = pos=(0,0,0) rot=(1,0,0;1.5708rad)
  Size = 0.16
FEATURE [PartDesign::Revolution] Revolution052
  Angle = 360
  Axis = (0,2e-16,1)
  Base = (0,0,0)
  Placement = pos=(0,0,0) rot=(1,0,0;1.5708rad)
  Profile = -> Sketch200
  ReferenceAxis = -> Sketch200 [V_Axis]
  Reversed = true
FEATURE [PartDesign::Pocket] Pocket115
  BaseFeature = -> Revolution052
  Length = 1
  Length2 = 100
  Placement = pos=(0,0,0) rot=(1,0,0;1.5708rad)
  Profile = -> Sketch201
  Reversed = true
  Type = 0
FEATURE [PartDesign::Revolution] Revolution053
  Angle = 360
  Axis = (0,2e-16,1)
  Base = (0,0,0)
  Placement = pos=(0,0,0) rot=(1,0,0;1.5708rad)
  Profile = -> Sketch213
  ReferenceAxis = -> Sketch213 [V_Axis]
  Reversed = true
FEATURE [PartDesign::Pocket] Pocket116
  BaseFeature = -> Pocket115
  Length = 0.25
  Length2 = 0.25
  Placement = pos=(0,0,0) rot=(1,0,0;1.5708rad)
  Profile = -> Sketch203
  Type = 4
FEATURE [PartDesign::Body] Body721  label="LED 5mm Head"
  Group = -> [Sketch200,Revolution052,Sketch201,Pocket115,Sketch203,Pocket116]
  Origin = -> Origin1021
  Tip = -> Pocket116
FEATURE [PartDesign::Pocket] Pocket120
  BaseFeature = -> Revolution053
  Length = 1
  Length2 = 100
  Placement = pos=(0,0,0) rot=(1,0,0;1.5708rad)
  Profile = -> Sketch214
  Reversed = true
  Type = 0
FEATURE [PartDesign::Pad] Pad064
  Length = 2
  Length2 = 100
  Profile = -> Sketch212
  Type = 0
FEATURE [Sketcher::SketchObject] Sketch209
  ExternalGeometry = -> [Pad064]
  MapMode = 5
  Placement = pos=(0,0,0) rot=(1,0,0;3.14159rad)
  Support = -> [Pad064]
  sketch-geometry (8):
    g0: LineSegment StartX=130.393 StartY=-23.7629 StartZ=0 EndX=146.893 EndY=-23.7629 EndZ=0
    g1: LineSegment StartX=146.893 StartY=-23.7629 StartZ=0 EndX=146.893 EndY=-29.5129 EndZ=0
    g2: LineSegment StartX=146.893 StartY=-40.2629 StartZ=0 EndX=130.393 EndY=-40.2629 EndZ=0
    g3: LineSegment StartX=130.393 StartY=-40.2629 StartZ=0 EndX=130.393 EndY=-34.5129 EndZ=0
    g4: ArcOfCircle CenterX=146.893 CenterY=-32.0129 CenterZ=0 NormalX=0 NormalY=0 NormalZ=1 AngleXU=0 Radius=2.5 StartAngle=4.71239 EndAngle=7.85398
    g5: ArcOfCircle CenterX=130.393 CenterY=-32.0129 CenterZ=0 NormalX=0 NormalY=0 NormalZ=1 AngleXU=0 Radius=2.5 StartAngle=1.5708 EndAngle=4.71239
    g6: LineSegment StartX=130.393 StartY=-29.5129 StartZ=0 EndX=130.393 EndY=-23.7629 EndZ=0
    g7: LineSegment StartX=146.893 StartY=-34.5129 StartZ=0 EndX=146.893 EndY=-40.2629 EndZ=0
  constraints (24):
    c: Coincident(g0,g1)
    c: Coincident(g7,g2)
    c: Coincident(g2,g3)
    c: Coincident(g6,g0)
    c: Horizontal(g0)
    c: Horizontal(g2)
    c: Vertical(g1)
    c: Vertical(g3)
    c: Coincident(g6,g5)
    c: Tangent(g3,g6)
    c: Coincident(g3,g5)
    c: Coincident(g4,g1)
    c: Coincident(g4,g7)
    c: Vertical(g7)
    c: Vertical(g4,g1)
    c: Equal(g5,g4)
    c: Symmetric(g0,g2,g4)
    c: Horizontal(g5,g4)
    c: Radius(g4) = 2.5
    c: DistanceX(g0,g0) = 16.5
    c: Vertical(g5,g3)
    c: DistanceX(g-4,g2) = 9.5
    c: DistanceY(g-4,g2) = 15
    c: DistanceY(g2,g0) = 16.5
FEATURE [PartDesign::Pad] Pad065
  BaseFeature = -> Pad064
  Length = 7
  Length2 = 100
  Profile = -> Sketch209
  Type = 0
FEATURE [Sketcher::SketchObject] Sketch208
  ExternalGeometry = -> [Pad065]
  MapMode = 5
  Placement = pos=(0,0,-7) rot=(1,0,0;3.14159rad)
  Support = -> [Pad065]
  sketch-geometry (2):
    g0: Circle CenterX=138.643 CenterY=-32.0129 CenterZ=0 NormalX=0 NormalY=0 NormalZ=1 AngleXU=0 Radius=8
    g1: LineSegment [constr] StartX=130.393 StartY=-23.7629 StartZ=0 EndX=146.893 EndY=-40.2629 EndZ=0
  constraints (4):
    c: Coincident(g1,g-4)
    c: Coincident(g1,g-5)
    c: Symmetric(g1,g1,g0)
    c: Radius(g0) = 8
FEATURE [PartDesign::Pad] Pad066
  BaseFeature = -> Pad065
  Length = 3
  Length2 = 100
  Profile = -> Sketch208
  Type = 0
FEATURE [Sketcher::SketchObject] Sketch210
  ExternalGeometry = -> [Pad066]
  MapMode = 5
  Placement = pos=(0,0,-10) rot=(1,0,0;3.14159rad)
  Support = -> [Pad066]
  sketch-geometry (1):
    g0: Circle CenterX=138.643 CenterY=-32.0129 CenterZ=0 NormalX=0 NormalY=0 NormalZ=1 AngleXU=0 Radius=6
  constraints (2):
    c: Coincident(g0,g-3)
    c: Radius(g0) = 6
FEATURE [PartDesign::Pad] Pad063
  BaseFeature = -> Pad066
  Length = 4
  Length2 = 100
  Profile = -> Sketch210
  Type = 0
FEATURE [Sketcher::SketchObject] Sketch207
  ExternalGeometry = -> [Pad063]
  MapMode = 5
  Placement = pos=(0,0,-14) rot=(1,0,0;3.14159rad)
  Support = -> [Pad063]
  sketch-geometry (1):
    g0: Circle CenterX=138.643 CenterY=-32.0129 CenterZ=0 NormalX=0 NormalY=0 NormalZ=1 AngleXU=0 Radius=7.5
  constraints (2):
    c: Coincident(g0,g-3)
    c: Radius(g0) = 7.5
FEATURE [PartDesign::Pad] Pad062
  BaseFeature = -> Pad063
  Length = 4.5
  Length2 = 100
  Profile = -> Sketch207
  Type = 0
FEATURE [Sketcher::SketchObject] Sketch211
  ExternalGeometry = -> [Pad062]
  MapMode = 5
  Placement = pos=(0,0,-18.5) rot=(1,0,0;3.14159rad)
  Support = -> [Pad062]
  sketch-geometry (1):
    g0: Circle CenterX=138.643 CenterY=-32.0129 CenterZ=0 NormalX=0 NormalY=0 NormalZ=1 AngleXU=0 Radius=5
  constraints (2):
    c: Coincident(g0,g-3)
    c: Radius(g0) = 5
FEATURE [PartDesign::Pocket] Pocket118
  BaseFeature = -> Pad062
  Length = 1
  Length2 = 100
  Profile = -> Sketch211
  Type = 0
FEATURE [PartDesign::Pocket] Pocket117
  BaseFeature = -> Pocket118
  Length = 2
  Length2 = 100
  Profile = -> Pocket118 [Face27]
  Type = 0
FEATURE [PartDesign::Pad] Pad058
  Length = 0.25
  Length2 = 0.25
  Placement = pos=(0,0,0) rot=(1,0,0;1.5708rad)
  Profile = -> Sketch202
  Type = 4
FEATURE [PartDesign::Body] Body720  label="LED 5mm Pins"
  Group = -> [Sketch202,Pad058]
  Origin = -> Origin1019
  Tip = -> Pad058
FEATURE [PartDesign::Pad] Pad059
  Length = 2
  Length2 = 100
  Profile = -> Sketch204
  Type = 0
FEATURE [PartDesign::Pocket] Pocket119
  BaseFeature = -> Pocket120
  Length = 0.25
  Length2 = 0.25
  Placement = pos=(0,0,0) rot=(1,0,0;1.5708rad)
  Profile = -> Sketch216
  Type = 4
FEATURE [PartDesign::Body] Body717  label="LED 5mm Head001"
  Group = -> [Sketch213,Revolution053,Sketch214,Pocket120,Sketch216,Pocket119]
  Origin = -> Origin1018
  Tip = -> Pocket119
FEATURE [PartDesign::Pad] Pad067
  Length = 0.25
  Length2 = 0.25
  Placement = pos=(0,0,0) rot=(1,0,0;1.5708rad)
  Profile = -> Sketch215
  Type = 4
FEATURE [PartDesign::Body] Body715  label="LED 5mm Pins001"
  Group = -> [Sketch215,Pad067]
  Origin = -> Origin1031
  Tip = -> Pad067
FEATURE [App::Part] Part281  label="LED 5mm #2"
  Group = -> [Body717,Body715]
  Origin = -> Origin1034
  Placement = pos=(66.05,-57.9183,10.0347) rot=(1,0,0;0.426558rad)
FEATURE [PartDesign::Revolution] Revolution054
  Angle = 360
  Axis = (0,2e-16,1)
  Base = (0,0,0)
  Placement = pos=(0,0,0) rot=(1,0,0;1.5708rad)
  Profile = -> Sketch217
  ReferenceAxis = -> Sketch217 [V_Axis]
  Reversed = true
FEATURE [PartDesign::Pocket] Pocket889
  BaseFeature = -> Revolution054
  Length = 1
  Length2 = 100
  Placement = pos=(0,0,0) rot=(1,0,0;1.5708rad)
  Profile = -> Sketch218
  Reversed = true
  Type = 0
FEATURE [PartDesign::Pocket] Pocket890
  BaseFeature = -> Pocket889
  Length = 0.25
  Length2 = 0.25
  Placement = pos=(0,0,0) rot=(1,0,0;1.5708rad)
  Profile = -> Sketch220
  Type = 4
FEATURE [PartDesign::Body] Body729  label="LED 5mm Head002"
  Group = -> [Sketch217,Revolution054,Sketch218,Pocket889,Sketch220,Pocket890]
  Origin = -> Origin055
  Tip = -> Pocket890
FEATURE [PartDesign::Pad] Pad070
  Length = 0.25
  Length2 = 0.25
  Placement = pos=(0,0,0) rot=(1,0,0;1.5708rad)
  Profile = -> Sketch227
  Type = 4
FEATURE [PartDesign::Body] Body718  label="LED 5mm Pins004"
  Group = -> [Sketch227,Pad070]
  Origin = -> Origin1030
  Tip = -> Pad070
FEATURE [PartDesign::Pad] Pad071
  Length = 0.25
  Length2 = 0.25
  Placement = pos=(0,0,0) rot=(1,0,0;1.5708rad)
  Profile = -> Sketch231
  Type = 4
FEATURE [PartDesign::Pad] Pad068
  Length = 0.25
  Length2 = 0.25
  Placement = pos=(0,0,0) rot=(1,0,0;1.5708rad)
  Profile = -> Sketch219
  Type = 4
FEATURE [PartDesign::Body] Body723  label="LED 5mm Pins002"
  Group = -> [Sketch219,Pad068]
  Origin = -> Origin056
  Tip = -> Pad068
FEATURE [PartDesign::Pad] Pad069
  Length = 0.25
  Length2 = 0.25
  Placement = pos=(0,0,0) rot=(1,0,0;1.5708rad)
  Profile = -> Sketch223
  Type = 4
FEATURE [PartDesign::Body] Body724  label="LED 5mm Pins003"
  Group = -> [Sketch223,Pad069]
  Origin = -> Origin1028
  Tip = -> Pad069
FEATURE [PartDesign::Revolution] Revolution055
  Angle = 360
  Axis = (0,2e-16,1)
  Base = (0,0,0)
  Placement = pos=(0,0,0) rot=(1,0,0;1.5708rad)
  Profile = -> Sketch221
  ReferenceAxis = -> Sketch221 [V_Axis]
  Reversed = true
FEATURE [PartDesign::Pocket] Pocket893
  BaseFeature = -> Revolution055
  Length = 1
  Length2 = 100
  Placement = pos=(0,0,0) rot=(1,0,0;1.5708rad)
  Profile = -> Sketch222
  Reversed = true
  Type = 0
FEATURE [PartDesign::Pocket] Pocket891
  BaseFeature = -> Pocket893
  Length = 0.25
  Length2 = 0.25
  Placement = pos=(0,0,0) rot=(1,0,0;1.5708rad)
  Profile = -> Sketch224
  Type = 4
FEATURE [PartDesign::Body] Body722  label="LED 5mm Head003"
  Group = -> [Sketch221,Revolution055,Sketch222,Pocket893,Sketch224,Pocket891]
  Origin = -> Origin1029
  Tip = -> Pocket891
FEATURE [PartDesign::Revolution] Revolution056
  Angle = 360
  Axis = (0,2e-16,1)
  Base = (0,0,0)
  Placement = pos=(0,0,0) rot=(1,0,0;1.5708rad)
  Profile = -> Sketch225
  ReferenceAxis = -> Sketch225 [V_Axis]
  Reversed = true
FEATURE [PartDesign::Pocket] Pocket895
  BaseFeature = -> Revolution056
  Length = 1
  Length2 = 100
  Placement = pos=(0,0,0) rot=(1,0,0;1.5708rad)
  Profile = -> Sketch226
  Reversed = true
  Type = 0
FEATURE [PartDesign::Pocket] Pocket894
  BaseFeature = -> Pocket895
  Length = 0.25
  Length2 = 0.25
  Placement = pos=(0,0,0) rot=(1,0,0;1.5708rad)
  Profile = -> Sketch228
  Type = 4
FEATURE [PartDesign::Body] Body716  label="LED 5mm Head004"
  Group = -> [Sketch225,Revolution056,Sketch226,Pocket895,Sketch228,Pocket894]
  Origin = -> Origin1025
  Tip = -> Pocket894
FEATURE [App::Part] Part283  label="LED 5mm #5"
  Group = -> [Body716,Body718]
  Origin = -> Origin1014
  Placement = pos=(48.05,-23.7345,10.0595) rot=(1,0,0;0.426558rad)
FEATURE [PartDesign::Revolution] Revolution057
  Angle = 360
  Axis = (0,2e-16,1)
  Base = (0,0,0)
  Placement = pos=(0,0,0) rot=(1,0,0;1.5708rad)
  Profile = -> Sketch229
  ReferenceAxis = -> Sketch229 [V_Axis]
  Reversed = true
FEATURE [PartDesign::Pocket] Pocket892
  BaseFeature = -> Revolution057
  Length = 1
  Length2 = 100
  Placement = pos=(0,0,0) rot=(1,0,0;1.5708rad)
  Profile = -> Sketch230
  Reversed = true
  Type = 0
FEATURE [PartDesign::Pocket] Pocket896
  BaseFeature = -> Pocket892
  Length = 0.25
  Length2 = 0.25
  Placement = pos=(0,0,0) rot=(1,0,0;1.5708rad)
  Profile = -> Sketch232
  Type = 4
FEATURE [PartDesign::Body] Body719  label="LED 5mm Head005"
  Group = -> [Sketch229,Revolution057,Sketch230,Pocket892,Sketch232,Pocket896]
  Origin = -> Origin1023
  Tip = -> Pocket896
FEATURE [PartDesign::Pad] Pad1103
  Length = 2
  Length2 = 100
  Profile = -> Sketch2451
  Type = 0
FEATURE [PartDesign::Body] Body725  label="HC-SR04 PCB"
  Group = -> [Sketch2451,Pad1103]
  Origin = -> Origin1056
  Tip = -> Pad1103
FEATURE [PartDesign::Pad] Pad1104
  Length = 3
  Length2 = 100
  Profile = -> Sketch2450
  Type = 0
FEATURE [PartDesign::Fillet] Fillet264
  Base = -> Pad1104 [Edge7]
  BaseFeature = -> Pad1104
  Radius = 0.3
FEATURE [PartDesign::Body] Body727  label="HC-SR04 Clock"
  Group = -> [Sketch2450,Pad1104,Fillet264]
  Origin = -> Origin1048
  Placement = pos=(0,0,2) rot=(0,0,1;0rad)
  Tip = -> Fillet264
FEATURE [PartDesign::Pad] Pad1106
  Length = 2.5
  Length2 = 100
  Profile = -> Sketch2465
  Type = 0
FEATURE [PartDesign::Chamfer] Chamfer568
  Base = -> Pad1106 [Edge2,Edge1,Edge5,Edge8]
  BaseFeature = -> Pad1106
  Size = 0.2
FEATURE [PartDesign::Chamfer] Chamfer570
  Base = -> Chamfer568 [Face5,Face2]
  BaseFeature = -> Chamfer568
  Size = 0.05
FEATURE [PartDesign::Body] Body730  label="Pin Header Block002"
  Group = -> [Sketch2465,Pad1106,Chamfer568,Chamfer570]
  Origin = -> Origin1045
  Tip = -> Chamfer570
FEATURE [Part::FeaturePython] Array002  # Draft array (typed FeaturePython)
  Angle = 360
  ArrayType = 0
  Axis = (0,0,1)
  Base = -> Body730
  Center = (0,0,0)
  Fuse = false
  IntervalAxis = (0,0,0)
  IntervalX = (2.54,0,0)
  IntervalY = (0,1,0)
  IntervalZ = (0,0,1)
  NumberPolar = 1
  NumberX = 4
  NumberY = 1
  NumberZ = 1
FEATURE [PartDesign::Pad] Pad1107
  Length = 0.32
  Length2 = 0.32
  Placement = pos=(0,0,0) rot=(1,0,0;1.5708rad)
  Profile = -> Sketch2505
  Type = 4
FEATURE [PartDesign::Chamfer] Chamfer569
  Base = -> Pad1107 [Face3,Face1]
  BaseFeature = -> Pad1107
  Placement = pos=(0,0,0) rot=(1,0,0;1.5708rad)
  Size = 0.16
FEATURE [PartDesign::Body] Body728  label="Pin Header Pin002"
  Group = -> [Sketch2505,Pad1107,Chamfer569]
  Origin = -> Origin1055
  Tip = -> Chamfer569
FEATURE [Part::FeaturePython] Array003  # Draft array (typed FeaturePython)
  Angle = 360
  ArrayType = 0
  Axis = (0,0,1)
  Base = -> Body728
  Center = (0,0,0)
  Fuse = false
  IntervalAxis = (0,0,0)
  IntervalX = (2.54,0,0)
  IntervalY = (0,1,0)
  IntervalZ = (0,0,1)
  NumberPolar = 1
  NumberX = 4
  NumberY = 1
  NumberZ = 1
FEATURE [App::Part] Part294  label="LED 5mm #3"
  Group = -> [Body729,Body723]
  Origin = -> Origin054
  Placement = pos=(75.05,-41.7437,12.2179) rot=(0.207078,-0.207078,0.956158;1.61561rad)
FEATURE [App::Part] Part295  label="Pin Header002"
  Group = -> [Body730,Body728,Array002,Array003]
  Origin = -> Origin1057
  Placement = pos=(3.8,-8.4,5e-16) rot=(0,1,0;3.14159rad)
FEATURE [App::Part] Part296  label="LED 5mm #1"
  Group = -> [Body721,Body720]
  Origin = -> Origin1012
  Placement = pos=(48.05,-57.8962,10.0441) rot=(-1,0,0;5.85663rad)
FEATURE [App::Part] Part297  label="LED 5mm #4"
  Group = -> [Body722,Body724]
  Origin = -> Origin1013
  Placement = pos=(66.1,-23.7354,10.0796) rot=(1,0,0;0.426558rad)
FEATURE [PartDesign::Pad] Pad1124  label="M3x8 Head171"
  Length = 3
  Length2 = 100
  Profile = -> Sketch2452
  Type = 0
FEATURE [Sketcher::SketchObject] Sketch2455
  MapMode = 5
  Placement = pos=(0,0,3) rot=(0,0,1;0rad)
  Support = -> [Pad1124]
  sketch-geometry (1):
    g0: Circle CenterX=0 CenterY=0 CenterZ=0 NormalX=0 NormalY=0 NormalZ=1 AngleXU=0 Radius=1.5
  constraints (2):
    c: Coincident(g0,g-1)
    c: Radius(g0) = 1.5
FEATURE [PartDesign::Pad] Pad1130  label="M3x8 Head175"
  Length = 3
  Length2 = 100
  Profile = -> Sketch2462
  Type = 0
FEATURE [Sketcher::SketchObject] Sketch2457
  MapMode = 5
  Placement = pos=(0,0,3) rot=(0,0,1;0rad)
  Support = -> [Pad1130]
  sketch-geometry (1):
    g0: Circle CenterX=0 CenterY=0 CenterZ=0 NormalX=0 NormalY=0 NormalZ=1 AngleXU=0 Radius=1.5
  constraints (2):
    c: Coincident(g0,g-1)
    c: Radius(g0) = 1.5
FEATURE [PartDesign::Pad] Pad1131  label="M3x8 Thread175"
  BaseFeature = -> Pad1124
  Length = 8
  Length2 = 100
  Profile = -> Sketch2455
  Type = 0
FEATURE [Sketcher::SketchObject] Sketch2454
  MapMode = 5
  Placement = pos=(0,0,0) rot=(1,0,0;3.14159rad)
  Support = -> [Pad1131]
  sketch-geometry (7):
    g0: LineSegment StartX=1.275 StartY=0.736122 StartZ=0 EndX=0 EndY=1.47224 EndZ=0
    g1: LineSegment StartX=0 StartY=1.47224 StartZ=0 EndX=-1.275 EndY=0.736122 EndZ=0
    g2: LineSegment StartX=-1.275 StartY=0.736122 StartZ=0 EndX=-1.275 EndY=-0.736122 EndZ=0
    g3: LineSegment StartX=-1.275 StartY=-0.736122 StartZ=0 EndX=1.34766e-11 EndY=-1.47224 EndZ=0
    g4: LineSegment StartX=1.34766e-11 StartY=-1.47224 StartZ=0 EndX=1.275 EndY=-0.736122 EndZ=0
    g5: LineSegment StartX=1.275 StartY=-0.736122 StartZ=0 EndX=1.275 EndY=0.736122 EndZ=0
    g6: Circle [constr] CenterX=0 CenterY=0 CenterZ=0 NormalX=0 NormalY=0 NormalZ=1 AngleXU=0 Radius=1.47224
  constraints (16):
    c: Coincident(g0,g1)
    c: Coincident(g1,g2)
    c: Coincident(g2,g3)
    c: Coincident(g3,g4)
    c: Coincident(g4,g5)
    c: Coincident(g5,g0)
    c: Equal(g0, g1-g5) x5
    c: PointOnObject(g0,g6)
    c: PointOnObject(g1,g6)
    c: PointOnObject(g2,g6)
    c: PointOnObject(g3,g6)
    c: PointOnObject(g4,g6)
    c: PointOnObject(g5,g6)
    c: Coincident(g6,g-1)
    c: PointOnObject(g0,g-2)
    c: DistanceX(g1,g0) = 2.55
FEATURE [PartDesign::Pocket] Pocket898  label="M3x8 Wrench172"
  BaseFeature = -> Pad1131
  Length = 1.3
  Length2 = 100
  Profile = -> Sketch2454
  Type = 0
FEATURE [PartDesign::Chamfer] Chamfer557  label="M3x8 Smooth175"
  Base = -> Pocket898 [Face11,Edge2,Edge24,Edge3]
  BaseFeature = -> Pocket898
  Size = 0.2
FEATURE [PartDesign::Pad] Pad1132  label="M3x8 Head176"
  Length = 3
  Length2 = 100
  Profile = -> Sketch2460
  Type = 0
FEATURE [Sketcher::SketchObject] Sketch2453
  MapMode = 5
  Placement = pos=(0,0,3) rot=(0,0,1;0rad)
  Support = -> [Pad1132]
  sketch-geometry (1):
    g0: Circle CenterX=0 CenterY=0 CenterZ=0 NormalX=0 NormalY=0 NormalZ=1 AngleXU=0 Radius=1.5
  constraints (2):
    c: Coincident(g0,g-1)
    c: Radius(g0) = 1.5
FEATURE [PartDesign::Pad] Pad1134  label="M3x8 Thread176"
  BaseFeature = -> Pad1132
  Length = 8
  Length2 = 100
  Profile = -> Sketch2453
  Type = 0
FEATURE [Sketcher::SketchObject] Sketch2456
  MapMode = 5
  Placement = pos=(0,0,0) rot=(1,0,0;3.14159rad)
  Support = -> [Pad1134]
  sketch-geometry (7):
    g0: LineSegment StartX=1.275 StartY=0.736122 StartZ=0 EndX=0 EndY=1.47224 EndZ=0
    g1: LineSegment StartX=0 StartY=1.47224 StartZ=0 EndX=-1.275 EndY=0.736122 EndZ=0
    g2: LineSegment StartX=-1.275 StartY=0.736122 StartZ=0 EndX=-1.275 EndY=-0.736122 EndZ=0
    g3: LineSegment StartX=-1.275 StartY=-0.736122 StartZ=0 EndX=1.34766e-11 EndY=-1.47224 EndZ=0
    g4: LineSegment StartX=1.34766e-11 StartY=-1.47224 StartZ=0 EndX=1.275 EndY=-0.736122 EndZ=0
    g5: LineSegment StartX=1.275 StartY=-0.736122 StartZ=0 EndX=1.275 EndY=0.736122 EndZ=0
    g6: Circle [constr] CenterX=0 CenterY=0 CenterZ=0 NormalX=0 NormalY=0 NormalZ=1 AngleXU=0 Radius=1.47224
  constraints (16):
    c: Coincident(g0,g1)
    c: Coincident(g1,g2)
    c: Coincident(g2,g3)
    c: Coincident(g3,g4)
    c: Coincident(g4,g5)
    c: Coincident(g5,g0)
    c: Equal(g0, g1-g5) x5
    c: PointOnObject(g0,g6)
    c: PointOnObject(g1,g6)
    c: PointOnObject(g2,g6)
    c: PointOnObject(g3,g6)
    c: PointOnObject(g4,g6)
    c: PointOnObject(g5,g6)
    c: Coincident(g6,g-1)
    c: PointOnObject(g0,g-2)
    c: DistanceX(g1,g0) = 2.55
FEATURE [PartDesign::Pocket] Pocket902  label="M3x8 Wrench176"
  BaseFeature = -> Pad1134
  Length = 1.3
  Length2 = 100
  Profile = -> Sketch2456
  Type = 0
FEATURE [PartDesign::Chamfer] Chamfer556  label="M3x8 Smooth174"
  Base = -> Pocket902 [Face11,Edge2,Edge24,Edge3]
  BaseFeature = -> Pocket902
  Size = 0.2
FEATURE [PartDesign::Pad] Pad1135  label="M3x8 Thread177"
  BaseFeature = -> Pad1130
  Length = 8
  Length2 = 100
  Profile = -> Sketch2457
  Type = 0
FEATURE [Sketcher::SketchObject] Sketch2461
  MapMode = 5
  Placement = pos=(0,0,0) rot=(1,0,0;3.14159rad)
  Support = -> [Pad1135]
  sketch-geometry (7):
    g0: LineSegment StartX=1.275 StartY=0.736122 StartZ=0 EndX=0 EndY=1.47224 EndZ=0
    g1: LineSegment StartX=0 StartY=1.47224 StartZ=0 EndX=-1.275 EndY=0.736122 EndZ=0
    g2: LineSegment StartX=-1.275 StartY=0.736122 StartZ=0 EndX=-1.275 EndY=-0.736122 EndZ=0
    g3: LineSegment StartX=-1.275 StartY=-0.736122 StartZ=0 EndX=1.34766e-11 EndY=-1.47224 EndZ=0
    g4: LineSegment StartX=1.34766e-11 StartY=-1.47224 StartZ=0 EndX=1.275 EndY=-0.736122 EndZ=0
    g5: LineSegment StartX=1.275 StartY=-0.736122 StartZ=0 EndX=1.275 EndY=0.736122 EndZ=0
    g6: Circle [constr] CenterX=0 CenterY=0 CenterZ=0 NormalX=0 NormalY=0 NormalZ=1 AngleXU=0 Radius=1.47224
  constraints (16):
    c: Coincident(g0,g1)
    c: Coincident(g1,g2)
    c: Coincident(g2,g3)
    c: Coincident(g3,g4)
    c: Coincident(g4,g5)
    c: Coincident(g5,g0)
    c: Equal(g0, g1-g5) x5
    c: PointOnObject(g0,g6)
    c: PointOnObject(g1,g6)
    c: PointOnObject(g2,g6)
    c: PointOnObject(g3,g6)
    c: PointOnObject(g4,g6)
    c: PointOnObject(g5,g6)
    c: Coincident(g6,g-1)
    c: PointOnObject(g0,g-2)
    c: DistanceX(g1,g0) = 2.55
FEATURE [PartDesign::Pocket] Pocket903  label="M3x8 Wrench177"
  BaseFeature = -> Pad1135
  Length = 1.3
  Length2 = 100
  Profile = -> Sketch2461
  Type = 0
FEATURE [PartDesign::Chamfer] Chamfer550  label="M3x8 Smooth172"
  Base = -> Pocket903 [Face11,Edge2,Edge24,Edge3]
  BaseFeature = -> Pocket903
  Size = 0.2
FEATURE [PartDesign::Pad] Pad1136  label="M3x8 Head178"
  Length = 3
  Length2 = 100
  Profile = -> Sketch2459
  Type = 0
FEATURE [Sketcher::SketchObject] Sketch2463
  MapMode = 5
  Placement = pos=(0,0,3) rot=(0,0,1;0rad)
  Support = -> [Pad1136]
  sketch-geometry (1):
    g0: Circle CenterX=0 CenterY=0 CenterZ=0 NormalX=0 NormalY=0 NormalZ=1 AngleXU=0 Radius=1.5
  constraints (2):
    c: Coincident(g0,g-1)
    c: Radius(g0) = 1.5
FEATURE [PartDesign::Pad] Pad1137  label="M3x8 Thread178"
  BaseFeature = -> Pad1136
  Length = 8
  Length2 = 100
  Profile = -> Sketch2463
  Type = 0
FEATURE [Sketcher::SketchObject] Sketch2458
  MapMode = 5
  Placement = pos=(0,0,0) rot=(1,0,0;3.14159rad)
  Support = -> [Pad1137]
  sketch-geometry (7):
    g0: LineSegment StartX=1.275 StartY=0.736122 StartZ=0 EndX=0 EndY=1.47224 EndZ=0
    g1: LineSegment StartX=0 StartY=1.47224 StartZ=0 EndX=-1.275 EndY=0.736122 EndZ=0
    g2: LineSegment StartX=-1.275 StartY=0.736122 StartZ=0 EndX=-1.275 EndY=-0.736122 EndZ=0
    g3: LineSegment StartX=-1.275 StartY=-0.736122 StartZ=0 EndX=1.34766e-11 EndY=-1.47224 EndZ=0
    g4: LineSegment StartX=1.34766e-11 StartY=-1.47224 StartZ=0 EndX=1.275 EndY=-0.736122 EndZ=0
    g5: LineSegment StartX=1.275 StartY=-0.736122 StartZ=0 EndX=1.275 EndY=0.736122 EndZ=0
    g6: Circle [constr] CenterX=0 CenterY=0 CenterZ=0 NormalX=0 NormalY=0 NormalZ=1 AngleXU=0 Radius=1.47224
  constraints (16):
    c: Coincident(g0,g1)
    c: Coincident(g1,g2)
    c: Coincident(g2,g3)
    c: Coincident(g3,g4)
    c: Coincident(g4,g5)
    c: Coincident(g5,g0)
    c: Equal(g0, g1-g5) x5
    c: PointOnObject(g0,g6)
    c: PointOnObject(g1,g6)
    c: PointOnObject(g2,g6)
    c: PointOnObject(g3,g6)
    c: PointOnObject(g4,g6)
    c: PointOnObject(g5,g6)
    c: Coincident(g6,g-1)
    c: PointOnObject(g0,g-2)
    c: DistanceX(g1,g0) = 2.55
FEATURE [PartDesign::Pocket] Pocket904  label="M3x8 Wrench178"
  BaseFeature = -> Pad1137
  Length = 1.3
  Length2 = 100
  Profile = -> Sketch2458
  Type = 0
FEATURE [PartDesign::Chamfer] Chamfer563  label="M3x8 Smooth176"
  Base = -> Pocket904 [Face11,Edge2,Edge24,Edge3]
  BaseFeature = -> Pocket904
  Size = 0.2
FEATURE [PartDesign::Body] Body735  label="OV7670 PCB"
  Group = -> [Sketch204,Pad059]
  Origin = -> Origin1017
  Tip = -> Pad059
FEATURE [PartDesign::Body] Body736  label="Pin Header Block"
  Group = -> [Sketch205,Pad060,Chamfer558,Chamfer561]
  Origin = -> Origin1016
  Tip = -> Chamfer561
FEATURE [Part::FeaturePython] Array  # Draft array (typed FeaturePython)
  Angle = 360
  ArrayType = 0
  Axis = (0,0,1)
  Base = -> Body736
  Center = (0,0,0)
  Fuse = false
  IntervalAxis = (0,0,0)
  IntervalX = (2.54,0,0)
  IntervalY = (0,2.54,0)
  IntervalZ = (0,0,1)
  NumberPolar = 1
  NumberX = 9
  NumberY = 2
  NumberZ = 1
FEATURE [PartDesign::Body] Body737  label="Kamera002"
  Group = -> [Sketch212,Pad064,Sketch209,Pad065,Sketch208,Pad066,Sketch210,Pad063,Sketch207,Pad062,Sketch211,Pocket118,Pocket117]
  Origin = -> Origin1032
  Tip = -> Pocket117
FEATURE [PartDesign::Body] Body738  label="OV7670 Pins"
  Origin = -> Origin1022
FEATURE [PartDesign::Body] Body739  label="Pin Header Pin"
  Group = -> [Sketch206,Pad061,Chamfer559]
  Origin = -> Origin1033
  Tip = -> Chamfer559
FEATURE [Part::FeaturePython] Array001  # Draft array (typed FeaturePython)
  Angle = 360
  ArrayType = 0
  Axis = (0,0,1)
  Base = -> Body739
  Center = (0,0,0)
  Fuse = false
  IntervalAxis = (0,0,0)
  IntervalX = (2.54,0,0)
  IntervalY = (0,2.54,0)
  IntervalZ = (0,0,1)
  NumberPolar = 1
  NumberX = 9
  NumberY = 2
  NumberZ = 1
FEATURE [App::Part] Part291  label="Pin Header"
  Group = -> [Body736,Array,Body739,Array001]
  Origin = -> Origin1027
  Placement = pos=(128.25,44.75,2) rot=(0,0,1;0rad)
FEATURE [App::Part] Part290  label="OV7670 (dirty CAD)"
  Group = -> [Body737,Body735,Body738,Part291]
  Origin = -> Origin1015
  Placement = pos=(-81.25,-32.1639,74.5199) rot=(1,0,0;0.426558rad)
FEATURE [PartDesign::Body] Body746  label="LED 5mm Pins005"
  Group = -> [Sketch231,Pad071]
  Origin = -> Origin1024
  Tip = -> Pad071
FEATURE [App::Part] Part287  label="LED 5mm #6"
  Group = -> [Body719,Body746]
  Origin = -> Origin1020
  Placement = pos=(38.95,-41.726,12.2072) rot=(-0.207078,0.207078,-0.956158;4.66757rad)
FEATURE [App::Part] Part285  label="White LEDs"
  Group = -> [Part296,Part281,Part294,Part297,Part283,Part287]
  Origin = -> Origin1026
  Placement = pos=(0,-39.0984,86.0323) rot=(1,0,0;3.14159rad)
FEATURE [App::Part] Part292  label="Sensormount LEDs"
  Group = -> [Part285,Body712]
  Origin = -> Origin1081
FEATURE [PartDesign::Body] Body755  label="M3x147"
  Group = -> [Sketch2460,Pad1132,Sketch2453,Pad1134,Sketch2456,Pocket902,Chamfer556]
  Origin = -> Origin1073
  Placement = pos=(100,-20.5,0) rot=(0,0,1;0rad)
  Tip = -> Chamfer556
FEATURE [PartDesign::Body] Body756  label="M3x148"
  Group = -> [Sketch2462,Pad1130,Sketch2457,Pad1135,Sketch2461,Pocket903,Chamfer550]
  Origin = -> Origin1077
  Placement = pos=(14,-48.5,0) rot=(0,0,1;0rad)
  Tip = -> Chamfer550
FEATURE [Sketcher::SketchObject] Sketch2509
  MapMode = 5
  Support = -> [XY_Plane1075]
  sketch-geometry (8):
    g0: LineSegment StartX=0 StartY=3.17543 StartZ=0 EndX=-2.75 EndY=1.58771 EndZ=0
    g1: LineSegment StartX=-2.75 StartY=1.58771 StartZ=0 EndX=-2.75 EndY=-1.58771 EndZ=0
    g2: LineSegment StartX=-2.75 StartY=-1.58771 StartZ=0 EndX=0 EndY=-3.17543 EndZ=0
    g3: LineSegment StartX=0 StartY=-3.17543 StartZ=0 EndX=2.75 EndY=-1.58771 EndZ=0
    g4: LineSegment StartX=2.75 StartY=-1.58771 StartZ=0 EndX=2.75 EndY=1.58771 EndZ=0
    g5: LineSegment StartX=2.75 StartY=1.58771 StartZ=0 EndX=0 EndY=3.17543 EndZ=0
    g6: Circle [constr] CenterX=0 CenterY=0 CenterZ=0 NormalX=0 NormalY=0 NormalZ=1 AngleXU=0 Radius=3.17543
    g7: Circle CenterX=0 CenterY=0 CenterZ=0 NormalX=0 NormalY=0 NormalZ=1 AngleXU=0 Radius=1.5
  constraints (18):
    c: Coincident(g0,g1)
    c: Coincident(g1,g2)
    c: Coincident(g2,g3)
    c: Coincident(g3,g4)
    c: Coincident(g4,g5)
    c: Coincident(g5,g0)
    c: Equal(g0, g1-g5) x5
    c: PointOnObject(g0,g6)
    c: PointOnObject(g1,g6)
    c: PointOnObject(g2,g6)
    c: PointOnObject(g3,g6)
    c: PointOnObject(g4,g6)
    c: PointOnObject(g5,g6)
    c: Coincident(g6,g-1)
    c: PointOnObject(g5,g-2)
    c: DistanceX(g0,g4) = 5.5
    c: Coincident(g7,g-1)
    c: Radius(g7) = 1.5
FEATURE [PartDesign::Pad] Pad1119  label="M3 Nut Primitive226"
  Length = 1.2
  Length2 = 1.2
  Profile = -> Sketch2509
  Type = 4
FEATURE [Sketcher::SketchObject] Sketch2510
  MapMode = 5
  Support = -> [XY_Plane1008]
  sketch-geometry (8):
    g0: LineSegment StartX=0 StartY=3.17543 StartZ=0 EndX=-2.75 EndY=1.58771 EndZ=0
    g1: LineSegment StartX=-2.75 StartY=1.58771 StartZ=0 EndX=-2.75 EndY=-1.58771 EndZ=0
    g2: LineSegment StartX=-2.75 StartY=-1.58771 StartZ=0 EndX=0 EndY=-3.17543 EndZ=0
    g3: LineSegment StartX=0 StartY=-3.17543 StartZ=0 EndX=2.75 EndY=-1.58771 EndZ=0
    g4: LineSegment StartX=2.75 StartY=-1.58771 StartZ=0 EndX=2.75 EndY=1.58771 EndZ=0
    g5: LineSegment StartX=2.75 StartY=1.58771 StartZ=0 EndX=0 EndY=3.17543 EndZ=0
    g6: Circle [constr] CenterX=0 CenterY=0 CenterZ=0 NormalX=0 NormalY=0 NormalZ=1 AngleXU=0 Radius=3.17543
    g7: Circle CenterX=0 CenterY=0 CenterZ=0 NormalX=0 NormalY=0 NormalZ=1 AngleXU=0 Radius=1.5
  constraints (18):
    c: Coincident(g0,g1)
    c: Coincident(g1,g2)
    c: Coincident(g2,g3)
    c: Coincident(g3,g4)
    c: Coincident(g4,g5)
    c: Coincident(g5,g0)
    c: Equal(g0, g1-g5) x5
    c: PointOnObject(g0,g6)
    c: PointOnObject(g1,g6)
    c: PointOnObject(g2,g6)
    c: PointOnObject(g3,g6)
    c: PointOnObject(g4,g6)
    c: PointOnObject(g5,g6)
    c: Coincident(g6,g-1)
    c: PointOnObject(g5,g-2)
    c: DistanceX(g0,g4) = 5.5
    c: Coincident(g7,g-1)
    c: Radius(g7) = 1.5
FEATURE [PartDesign::Pad] Pad1116  label="M3 Nut Primitive223"
  Length = 1.2
  Length2 = 1.2
  Profile = -> Sketch2510
  Type = 4
FEATURE [Sketcher::SketchObject] Sketch2511
  MapMode = 5
  Support = -> [XY_Plane1065]
  sketch-geometry (8):
    g0: LineSegment StartX=0 StartY=3.17543 StartZ=0 EndX=-2.75 EndY=1.58771 EndZ=0
    g1: LineSegment StartX=-2.75 StartY=1.58771 StartZ=0 EndX=-2.75 EndY=-1.58771 EndZ=0
    g2: LineSegment StartX=-2.75 StartY=-1.58771 StartZ=0 EndX=0 EndY=-3.17543 EndZ=0
    g3: LineSegment StartX=0 StartY=-3.17543 StartZ=0 EndX=2.75 EndY=-1.58771 EndZ=0
    g4: LineSegment StartX=2.75 StartY=-1.58771 StartZ=0 EndX=2.75 EndY=1.58771 EndZ=0
    g5: LineSegment StartX=2.75 StartY=1.58771 StartZ=0 EndX=0 EndY=3.17543 EndZ=0
    g6: Circle [constr] CenterX=0 CenterY=0 CenterZ=0 NormalX=0 NormalY=0 NormalZ=1 AngleXU=0 Radius=3.17543
    g7: Circle CenterX=0 CenterY=0 CenterZ=0 NormalX=0 NormalY=0 NormalZ=1 AngleXU=0 Radius=1.5
  constraints (18):
    c: Coincident(g0,g1)
    c: Coincident(g1,g2)
    c: Coincident(g2,g3)
    c: Coincident(g3,g4)
    c: Coincident(g4,g5)
    c: Coincident(g5,g0)
    c: Equal(g0, g1-g5) x5
    c: PointOnObject(g0,g6)
    c: PointOnObject(g1,g6)
    c: PointOnObject(g2,g6)
    c: PointOnObject(g3,g6)
    c: PointOnObject(g4,g6)
    c: PointOnObject(g5,g6)
    c: Coincident(g6,g-1)
    c: PointOnObject(g5,g-2)
    c: DistanceX(g0,g4) = 5.5
    c: Coincident(g7,g-1)
    c: Radius(g7) = 1.5
FEATURE [PartDesign::Pad] Pad1114  label="M3 Nut Primitive221"
  Length = 1.2
  Length2 = 1.2
  Profile = -> Sketch2511
  Type = 4
FEATURE [Sketcher::SketchObject] Sketch2508
  ExternalGeometry = -> [Pad1114]
  MapMode = 5
  Placement = pos=(0,0,0) rot=(0.57735,0.57735,0.57735;2.0944rad)
  Support = -> [YZ_Plane1063]
  sketch-geometry (6):
    g0: LineSegment StartX=-2.67543 StartY=1.2 StartZ=0 EndX=-3.67543 EndY=1.2 EndZ=0
    g1: LineSegment StartX=-3.67543 StartY=1.2 StartZ=0 EndX=-3.67543 EndY=-1.2 EndZ=0
    g2: LineSegment StartX=-3.67543 StartY=-1.2 StartZ=0 EndX=-2.67543 EndY=-1.2 EndZ=0
    g3: LineSegment StartX=-2.67543 StartY=-1.2 StartZ=0 EndX=-3.17543 EndY=-1 EndZ=0
    g4: LineSegment StartX=-3.17543 StartY=-1 StartZ=0 EndX=-3.17543 EndY=1 EndZ=0
    g5: LineSegment StartX=-3.17543 StartY=1 StartZ=0 EndX=-2.67543 EndY=1.2 EndZ=0
  constraints (15):
    c: Horizontal(g0)
    c: Coincident(g0,g1)
    c: Coincident(g1,g2)
    c: Coincident(g2,g3)
    c: Coincident(g3,g4)
    c: Coincident(g4,g5)
    c: Coincident(g5,g0)
    c: Symmetric(g4,g3,g-1)
    c: Symmetric(g0,g2,g-1)
    c: Symmetric(g1,g0,g-1)
    c: DistanceX(g0,g4) = 0.5
    c: DistanceY(g3,g4) = 2
    c: DistanceY(g1,g0) = 2.4
    c: PointOnObject(g3,g-3)
    c: DistanceX(g4,g0) = 0.5
FEATURE [PartDesign::Groove] Groove234  label="M3 Nut Smooth226"
  Angle = 360
  Axis = (-2e-16,3e-16,1)
  Base = (0,0,0)
  BaseFeature = -> Pad1114
  Profile = -> Sketch2508
  ReferenceAxis = -> Sketch2508 [V_Axis]
  Reversed = true
FEATURE [PartDesign::Chamfer] Chamfer554  label="M3 Nut Smooth Hole223"
  Base = -> Groove234 [Edge24,Edge23]
  BaseFeature = -> Groove234
  Size = 0.2
FEATURE [PartDesign::Body] Body750  label="M3 Nut131"
  Group = -> [Sketch2511,Pad1114,Sketch2508,Groove234,Chamfer554]
  Origin = -> Origin1040
  Placement = pos=(86,28,0) rot=(0,0,1;0rad)
  Tip = -> Chamfer554
FEATURE [Sketcher::SketchObject] Sketch2513
  MapMode = 5
  Support = -> [XY_Plane1074]
  sketch-geometry (8):
    g0: LineSegment StartX=0 StartY=3.17543 StartZ=0 EndX=-2.75 EndY=1.58771 EndZ=0
    g1: LineSegment StartX=-2.75 StartY=1.58771 StartZ=0 EndX=-2.75 EndY=-1.58771 EndZ=0
    g2: LineSegment StartX=-2.75 StartY=-1.58771 StartZ=0 EndX=0 EndY=-3.17543 EndZ=0
    g3: LineSegment StartX=0 StartY=-3.17543 StartZ=0 EndX=2.75 EndY=-1.58771 EndZ=0
    g4: LineSegment StartX=2.75 StartY=-1.58771 StartZ=0 EndX=2.75 EndY=1.58771 EndZ=0
    g5: LineSegment StartX=2.75 StartY=1.58771 StartZ=0 EndX=0 EndY=3.17543 EndZ=0
    g6: Circle [constr] CenterX=0 CenterY=0 CenterZ=0 NormalX=0 NormalY=0 NormalZ=1 AngleXU=0 Radius=3.17543
    g7: Circle CenterX=0 CenterY=0 CenterZ=0 NormalX=0 NormalY=0 NormalZ=1 AngleXU=0 Radius=1.5
  constraints (18):
    c: Coincident(g0,g1)
    c: Coincident(g1,g2)
    c: Coincident(g2,g3)
    c: Coincident(g3,g4)
    c: Coincident(g4,g5)
    c: Coincident(g5,g0)
    c: Equal(g0, g1-g5) x5
    c: PointOnObject(g0,g6)
    c: PointOnObject(g1,g6)
    c: PointOnObject(g2,g6)
    c: PointOnObject(g3,g6)
    c: PointOnObject(g4,g6)
    c: PointOnObject(g5,g6)
    c: Coincident(g6,g-1)
    c: PointOnObject(g5,g-2)
    c: DistanceX(g0,g4) = 5.5
    c: Coincident(g7,g-1)
    c: Radius(g7) = 1.5
FEATURE [PartDesign::Pad] Pad1120  label="M3 Nut Primitive227"
  Length = 1.2
  Length2 = 1.2
  Profile = -> Sketch2513
  Type = 4
FEATURE [Sketcher::SketchObject] Sketch2506
  ExternalGeometry = -> [Pad1120]
  MapMode = 5
  Placement = pos=(0,0,0) rot=(0.57735,0.57735,0.57735;2.0944rad)
  Support = -> [YZ_Plane1043]
  sketch-geometry (6):
    g0: LineSegment StartX=-2.67543 StartY=1.2 StartZ=0 EndX=-3.67543 EndY=1.2 EndZ=0
    g1: LineSegment StartX=-3.67543 StartY=1.2 StartZ=0 EndX=-3.67543 EndY=-1.2 EndZ=0
    g2: LineSegment StartX=-3.67543 StartY=-1.2 StartZ=0 EndX=-2.67543 EndY=-1.2 EndZ=0
    g3: LineSegment StartX=-2.67543 StartY=-1.2 StartZ=0 EndX=-3.17543 EndY=-1 EndZ=0
    g4: LineSegment StartX=-3.17543 StartY=-1 StartZ=0 EndX=-3.17543 EndY=1 EndZ=0
    g5: LineSegment StartX=-3.17543 StartY=1 StartZ=0 EndX=-2.67543 EndY=1.2 EndZ=0
  constraints (15):
    c: Horizontal(g0)
    c: Coincident(g0,g1)
    c: Coincident(g1,g2)
    c: Coincident(g2,g3)
    c: Coincident(g3,g4)
    c: Coincident(g4,g5)
    c: Coincident(g5,g0)
    c: Symmetric(g4,g3,g-1)
    c: Symmetric(g0,g2,g-1)
    c: Symmetric(g1,g0,g-1)
    c: DistanceX(g0,g4) = 0.5
    c: DistanceY(g3,g4) = 2
    c: DistanceY(g1,g0) = 2.4
    c: PointOnObject(g3,g-3)
    c: DistanceX(g4,g0) = 0.5
FEATURE [PartDesign::Groove] Groove230  label="M3 Nut Smooth222"
  Angle = 360
  Axis = (-2e-16,3e-16,1)
  Base = (0,0,0)
  BaseFeature = -> Pad1120
  Profile = -> Sketch2506
  ReferenceAxis = -> Sketch2506 [V_Axis]
  Reversed = true
FEATURE [PartDesign::Chamfer] Chamfer564  label="M3 Nut Smooth Hole226"
  Base = -> Groove230 [Edge24,Edge23]
  BaseFeature = -> Groove230
  Size = 0.2
FEATURE [PartDesign::Body] Body731  label="M3 Nut127"
  Group = -> [Sketch2513,Pad1120,Sketch2506,Groove230,Chamfer564]
  Origin = -> Origin1064
  Placement = pos=(57,-1.5,0) rot=(0,0,-1;1.5708rad)
  Tip = -> Chamfer564
FEATURE [Sketcher::SketchObject] Sketch2514
  MapMode = 5
  Support = -> [XY_Plane1080]
  sketch-geometry (8):
    g0: LineSegment StartX=0 StartY=3.17543 StartZ=0 EndX=-2.75 EndY=1.58771 EndZ=0
    g1: LineSegment StartX=-2.75 StartY=1.58771 StartZ=0 EndX=-2.75 EndY=-1.58771 EndZ=0
    g2: LineSegment StartX=-2.75 StartY=-1.58771 StartZ=0 EndX=0 EndY=-3.17543 EndZ=0
    g3: LineSegment StartX=0 StartY=-3.17543 StartZ=0 EndX=2.75 EndY=-1.58771 EndZ=0
    g4: LineSegment StartX=2.75 StartY=-1.58771 StartZ=0 EndX=2.75 EndY=1.58771 EndZ=0
    g5: LineSegment StartX=2.75 StartY=1.58771 StartZ=0 EndX=0 EndY=3.17543 EndZ=0
    g6: Circle [constr] CenterX=0 CenterY=0 CenterZ=0 NormalX=0 NormalY=0 NormalZ=1 AngleXU=0 Radius=3.17543
    g7: Circle CenterX=0 CenterY=0 CenterZ=0 NormalX=0 NormalY=0 NormalZ=1 AngleXU=0 Radius=1.5
  constraints (18):
    c: Coincident(g0,g1)
    c: Coincident(g1,g2)
    c: Coincident(g2,g3)
    c: Coincident(g3,g4)
    c: Coincident(g4,g5)
    c: Coincident(g5,g0)
    c: Equal(g0, g1-g5) x5
    c: PointOnObject(g0,g6)
    c: PointOnObject(g1,g6)
    c: PointOnObject(g2,g6)
    c: PointOnObject(g3,g6)
    c: PointOnObject(g4,g6)
    c: PointOnObject(g5,g6)
    c: Coincident(g6,g-1)
    c: PointOnObject(g5,g-2)
    c: DistanceX(g0,g4) = 5.5
    c: Coincident(g7,g-1)
    c: Radius(g7) = 1.5
FEATURE [PartDesign::Pad] Pad1118  label="M3 Nut Primitive225"
  Length = 1.2
  Length2 = 1.2
  Profile = -> Sketch2514
  Type = 4
FEATURE [Sketcher::SketchObject] Sketch2515
  ExternalGeometry = -> [Pad1118]
  MapMode = 5
  Placement = pos=(0,0,0) rot=(0.57735,0.57735,0.57735;2.0944rad)
  Support = -> [YZ_Plane1073]
  sketch-geometry (6):
    g0: LineSegment StartX=-2.67543 StartY=1.2 StartZ=0 EndX=-3.67543 EndY=1.2 EndZ=0
    g1: LineSegment StartX=-3.67543 StartY=1.2 StartZ=0 EndX=-3.67543 EndY=-1.2 EndZ=0
    g2: LineSegment StartX=-3.67543 StartY=-1.2 StartZ=0 EndX=-2.67543 EndY=-1.2 EndZ=0
    g3: LineSegment StartX=-2.67543 StartY=-1.2 StartZ=0 EndX=-3.17543 EndY=-1 EndZ=0
    g4: LineSegment StartX=-3.17543 StartY=-1 StartZ=0 EndX=-3.17543 EndY=1 EndZ=0
    g5: LineSegment StartX=-3.17543 StartY=1 StartZ=0 EndX=-2.67543 EndY=1.2 EndZ=0
  constraints (15):
    c: Horizontal(g0)
    c: Coincident(g0,g1)
    c: Coincident(g1,g2)
    c: Coincident(g2,g3)
    c: Coincident(g3,g4)
    c: Coincident(g4,g5)
    c: Coincident(g5,g0)
    c: Symmetric(g4,g3,g-1)
    c: Symmetric(g0,g2,g-1)
    c: Symmetric(g1,g0,g-1)
    c: DistanceX(g0,g4) = 0.5
    c: DistanceY(g3,g4) = 2
    c: DistanceY(g1,g0) = 2.4
    c: PointOnObject(g3,g-3)
    c: DistanceX(g4,g0) = 0.5
FEATURE [PartDesign::Groove] Groove229  label="M3 Nut Smooth221"
  Angle = 360
  Axis = (-2e-16,3e-16,1)
  Base = (0,0,0)
  BaseFeature = -> Pad1118
  Profile = -> Sketch2515
  ReferenceAxis = -> Sketch2515 [V_Axis]
  Reversed = true
FEATURE [PartDesign::Chamfer] Chamfer567  label="M3 Nut Smooth Hole228"
  Base = -> Groove229 [Edge24,Edge23]
  BaseFeature = -> Groove229
  Size = 0.2
FEATURE [PartDesign::Body] Body732  label="M3 Nut128"
  Group = -> [Sketch2514,Pad1118,Sketch2515,Groove229,Chamfer567]
  Origin = -> Origin1068
  Placement = pos=(57.5,28,0) rot=(0,0,-1;1.5708rad)
  Tip = -> Chamfer567
FEATURE [Sketcher::SketchObject] Sketch2516
  ExternalGeometry = -> [Pad1116]
  MapMode = 5
  Placement = pos=(0,0,0) rot=(0.57735,0.57735,0.57735;2.0944rad)
  Support = -> [YZ_Plane1002]
  sketch-geometry (6):
    g0: LineSegment StartX=-2.67543 StartY=1.2 StartZ=0 EndX=-3.67543 EndY=1.2 EndZ=0
    g1: LineSegment StartX=-3.67543 StartY=1.2 StartZ=0 EndX=-3.67543 EndY=-1.2 EndZ=0
    g2: LineSegment StartX=-3.67543 StartY=-1.2 StartZ=0 EndX=-2.67543 EndY=-1.2 EndZ=0
    g3: LineSegment StartX=-2.67543 StartY=-1.2 StartZ=0 EndX=-3.17543 EndY=-1 EndZ=0
    g4: LineSegment StartX=-3.17543 StartY=-1 StartZ=0 EndX=-3.17543 EndY=1 EndZ=0
    g5: LineSegment StartX=-3.17543 StartY=1 StartZ=0 EndX=-2.67543 EndY=1.2 EndZ=0
  constraints (15):
    c: Horizontal(g0)
    c: Coincident(g0,g1)
    c: Coincident(g1,g2)
    c: Coincident(g2,g3)
    c: Coincident(g3,g4)
    c: Coincident(g4,g5)
    c: Coincident(g5,g0)
    c: Symmetric(g4,g3,g-1)
    c: Symmetric(g0,g2,g-1)
    c: Symmetric(g1,g0,g-1)
    c: DistanceX(g0,g4) = 0.5
    c: DistanceY(g3,g4) = 2
    c: DistanceY(g1,g0) = 2.4
    c: PointOnObject(g3,g-3)
    c: DistanceX(g4,g0) = 0.5
FEATURE [PartDesign::Groove] Groove231  label="M3 Nut Smooth223"
  Angle = 360
  Axis = (-2e-16,3e-16,1)
  Base = (0,0,0)
  BaseFeature = -> Pad1116
  Profile = -> Sketch2516
  ReferenceAxis = -> Sketch2516 [V_Axis]
  Reversed = true
FEATURE [PartDesign::Chamfer] Chamfer546  label="M3 Nut Smooth Hole221"
  Base = -> Groove231 [Edge24,Edge23]
  BaseFeature = -> Groove231
  Size = 0.2
FEATURE [PartDesign::Body] Body707  label="M3 Nut125"
  Group = -> [Sketch2510,Pad1116,Sketch2516,Groove231,Chamfer546]
  Origin = -> Origin1047
  Placement = pos=(86,0,0) rot=(0,0,1;0rad)
  Tip = -> Chamfer546
FEATURE [Sketcher::SketchObject] Sketch2517
  MapMode = 5
  Support = -> [XY_Plane1068]
  sketch-geometry (8):
    g0: LineSegment StartX=0 StartY=3.17543 StartZ=0 EndX=-2.75 EndY=1.58771 EndZ=0
    g1: LineSegment StartX=-2.75 StartY=1.58771 StartZ=0 EndX=-2.75 EndY=-1.58771 EndZ=0
    g2: LineSegment StartX=-2.75 StartY=-1.58771 StartZ=0 EndX=0 EndY=-3.17543 EndZ=0
    g3: LineSegment StartX=0 StartY=-3.17543 StartZ=0 EndX=2.75 EndY=-1.58771 EndZ=0
    g4: LineSegment StartX=2.75 StartY=-1.58771 StartZ=0 EndX=2.75 EndY=1.58771 EndZ=0
    g5: LineSegment StartX=2.75 StartY=1.58771 StartZ=0 EndX=0 EndY=3.17543 EndZ=0
    g6: Circle [constr] CenterX=0 CenterY=0 CenterZ=0 NormalX=0 NormalY=0 NormalZ=1 AngleXU=0 Radius=3.17543
    g7: Circle CenterX=0 CenterY=0 CenterZ=0 NormalX=0 NormalY=0 NormalZ=1 AngleXU=0 Radius=1.5
  constraints (18):
    c: Coincident(g0,g1)
    c: Coincident(g1,g2)
    c: Coincident(g2,g3)
    c: Coincident(g3,g4)
    c: Coincident(g4,g5)
    c: Coincident(g5,g0)
    c: Equal(g0, g1-g5) x5
    c: PointOnObject(g0,g6)
    c: PointOnObject(g1,g6)
    c: PointOnObject(g2,g6)
    c: PointOnObject(g3,g6)
    c: PointOnObject(g4,g6)
    c: PointOnObject(g5,g6)
    c: Coincident(g6,g-1)
    c: PointOnObject(g5,g-2)
    c: DistanceX(g0,g4) = 5.5
    c: Coincident(g7,g-1)
    c: Radius(g7) = 1.5
FEATURE [PartDesign::Pad] Pad1117  label="M3 Nut Primitive224"
  Length = 1.2
  Length2 = 1.2
  Profile = -> Sketch2517
  Type = 4
FEATURE [Sketcher::SketchObject] Sketch2507
  ExternalGeometry = -> [Pad1117]
  MapMode = 5
  Placement = pos=(0,0,0) rot=(0.57735,0.57735,0.57735;2.0944rad)
  Support = -> [YZ_Plane1061]
  sketch-geometry (6):
    g0: LineSegment StartX=-2.67543 StartY=1.2 StartZ=0 EndX=-3.67543 EndY=1.2 EndZ=0
    g1: LineSegment StartX=-3.67543 StartY=1.2 StartZ=0 EndX=-3.67543 EndY=-1.2 EndZ=0
    g2: LineSegment StartX=-3.67543 StartY=-1.2 StartZ=0 EndX=-2.67543 EndY=-1.2 EndZ=0
    g3: LineSegment StartX=-2.67543 StartY=-1.2 StartZ=0 EndX=-3.17543 EndY=-1 EndZ=0
    g4: LineSegment StartX=-3.17543 StartY=-1 StartZ=0 EndX=-3.17543 EndY=1 EndZ=0
    g5: LineSegment StartX=-3.17543 StartY=1 StartZ=0 EndX=-2.67543 EndY=1.2 EndZ=0
  constraints (15):
    c: Horizontal(g0)
    c: Coincident(g0,g1)
    c: Coincident(g1,g2)
    c: Coincident(g2,g3)
    c: Coincident(g3,g4)
    c: Coincident(g4,g5)
    c: Coincident(g5,g0)
    c: Symmetric(g4,g3,g-1)
    c: Symmetric(g0,g2,g-1)
    c: Symmetric(g1,g0,g-1)
    c: DistanceX(g0,g4) = 0.5
    c: DistanceY(g3,g4) = 2
    c: DistanceY(g1,g0) = 2.4
    c: PointOnObject(g3,g-3)
    c: DistanceX(g4,g0) = 0.5
FEATURE [PartDesign::Groove] Groove233  label="M3 Nut Smooth225"
  Angle = 360
  Axis = (-2e-16,3e-16,1)
  Base = (0,0,0)
  BaseFeature = -> Pad1117
  Profile = -> Sketch2507
  ReferenceAxis = -> Sketch2507 [V_Axis]
  Reversed = true
FEATURE [PartDesign::Chamfer] Chamfer549  label="M3 Nut Smooth Hole222"
  Base = -> Groove233 [Edge24,Edge23]
  BaseFeature = -> Groove233
  Size = 0.2
FEATURE [PartDesign::Body] Body751  label="M3 Nut132"
  Group = -> [Sketch2517,Pad1117,Sketch2507,Groove233,Chamfer549]
  Origin = -> Origin1061
  Placement = pos=(0,28,0) rot=(0,0,1;0rad)
  Tip = -> Chamfer549
FEATURE [Sketcher::SketchObject] Sketch2518
  MapMode = 5
  Support = -> [XY_Plane1072]
  sketch-geometry (8):
    g0: LineSegment StartX=0 StartY=3.17543 StartZ=0 EndX=-2.75 EndY=1.58771 EndZ=0
    g1: LineSegment StartX=-2.75 StartY=1.58771 StartZ=0 EndX=-2.75 EndY=-1.58771 EndZ=0
    g2: LineSegment StartX=-2.75 StartY=-1.58771 StartZ=0 EndX=0 EndY=-3.17543 EndZ=0
    g3: LineSegment StartX=0 StartY=-3.17543 StartZ=0 EndX=2.75 EndY=-1.58771 EndZ=0
    g4: LineSegment StartX=2.75 StartY=-1.58771 StartZ=0 EndX=2.75 EndY=1.58771 EndZ=0
    g5: LineSegment StartX=2.75 StartY=1.58771 StartZ=0 EndX=0 EndY=3.17543 EndZ=0
    g6: Circle [constr] CenterX=0 CenterY=0 CenterZ=0 NormalX=0 NormalY=0 NormalZ=1 AngleXU=0 Radius=3.17543
    g7: Circle CenterX=0 CenterY=0 CenterZ=0 NormalX=0 NormalY=0 NormalZ=1 AngleXU=0 Radius=1.5
  constraints (18):
    c: Coincident(g0,g1)
    c: Coincident(g1,g2)
    c: Coincident(g2,g3)
    c: Coincident(g3,g4)
    c: Coincident(g4,g5)
    c: Coincident(g5,g0)
    c: Equal(g0, g1-g5) x5
    c: PointOnObject(g0,g6)
    c: PointOnObject(g1,g6)
    c: PointOnObject(g2,g6)
    c: PointOnObject(g3,g6)
    c: PointOnObject(g4,g6)
    c: PointOnObject(g5,g6)
    c: Coincident(g6,g-1)
    c: PointOnObject(g5,g-2)
    c: DistanceX(g0,g4) = 5.5
    c: Coincident(g7,g-1)
    c: Radius(g7) = 1.5
FEATURE [PartDesign::Pad] Pad1121  label="M3 Nut Primitive228"
  Length = 1.2
  Length2 = 1.2
  Profile = -> Sketch2518
  Type = 4
FEATURE [Sketcher::SketchObject] Sketch2512
  ExternalGeometry = -> [Pad1121]
  MapMode = 5
  Placement = pos=(0,0,0) rot=(0.57735,0.57735,0.57735;2.0944rad)
  Support = -> [YZ_Plane1069]
  sketch-geometry (6):
    g0: LineSegment StartX=-2.67543 StartY=1.2 StartZ=0 EndX=-3.67543 EndY=1.2 EndZ=0
    g1: LineSegment StartX=-3.67543 StartY=1.2 StartZ=0 EndX=-3.67543 EndY=-1.2 EndZ=0
    g2: LineSegment StartX=-3.67543 StartY=-1.2 StartZ=0 EndX=-2.67543 EndY=-1.2 EndZ=0
    g3: LineSegment StartX=-2.67543 StartY=-1.2 StartZ=0 EndX=-3.17543 EndY=-1 EndZ=0
    g4: LineSegment StartX=-3.17543 StartY=-1 StartZ=0 EndX=-3.17543 EndY=1 EndZ=0
    g5: LineSegment StartX=-3.17543 StartY=1 StartZ=0 EndX=-2.67543 EndY=1.2 EndZ=0
  constraints (15):
    c: Horizontal(g0)
    c: Coincident(g0,g1)
    c: Coincident(g1,g2)
    c: Coincident(g2,g3)
    c: Coincident(g3,g4)
    c: Coincident(g4,g5)
    c: Coincident(g5,g0)
    c: Symmetric(g4,g3,g-1)
    c: Symmetric(g0,g2,g-1)
    c: Symmetric(g1,g0,g-1)
    c: DistanceX(g0,g4) = 0.5
    c: DistanceY(g3,g4) = 2
    c: DistanceY(g1,g0) = 2.4
    c: PointOnObject(g3,g-3)
    c: DistanceX(g4,g0) = 0.5
FEATURE [PartDesign::Groove] Groove236  label="M3 Nut Smooth228"
  Angle = 360
  Axis = (-2e-16,3e-16,1)
  Base = (0,0,0)
  BaseFeature = -> Pad1121
  Profile = -> Sketch2512
  ReferenceAxis = -> Sketch2512 [V_Axis]
  Reversed = true
FEATURE [PartDesign::Chamfer] Chamfer562  label="M3 Nut Smooth Hole225"
  Base = -> Groove236 [Edge24,Edge23]
  BaseFeature = -> Groove236
  Size = 0.2
FEATURE [PartDesign::Body] Body733  label="M3 Nut129"
  Group = -> [Sketch2518,Pad1121,Sketch2512,Groove236,Chamfer562]
  Origin = -> Origin1065
  Placement = pos=(29,28,0) rot=(0,0,-1;1.5708rad)
  Tip = -> Chamfer562
FEATURE [Sketcher::SketchObject] Sketch2519
  ExternalGeometry = -> [Pad1119]
  MapMode = 5
  Placement = pos=(0,0,0) rot=(0.57735,0.57735,0.57735;2.0944rad)
  Support = -> [YZ_Plane1067]
  sketch-geometry (6):
    g0: LineSegment StartX=-2.67543 StartY=1.2 StartZ=0 EndX=-3.67543 EndY=1.2 EndZ=0
    g1: LineSegment StartX=-3.67543 StartY=1.2 StartZ=0 EndX=-3.67543 EndY=-1.2 EndZ=0
    g2: LineSegment StartX=-3.67543 StartY=-1.2 StartZ=0 EndX=-2.67543 EndY=-1.2 EndZ=0
    g3: LineSegment StartX=-2.67543 StartY=-1.2 StartZ=0 EndX=-3.17543 EndY=-1 EndZ=0
    g4: LineSegment StartX=-3.17543 StartY=-1 StartZ=0 EndX=-3.17543 EndY=1 EndZ=0
    g5: LineSegment StartX=-3.17543 StartY=1 StartZ=0 EndX=-2.67543 EndY=1.2 EndZ=0
  constraints (15):
    c: Horizontal(g0)
    c: Coincident(g0,g1)
    c: Coincident(g1,g2)
    c: Coincident(g2,g3)
    c: Coincident(g3,g4)
    c: Coincident(g4,g5)
    c: Coincident(g5,g0)
    c: Symmetric(g4,g3,g-1)
    c: Symmetric(g0,g2,g-1)
    c: Symmetric(g1,g0,g-1)
    c: DistanceX(g0,g4) = 0.5
    c: DistanceY(g3,g4) = 2
    c: DistanceY(g1,g0) = 2.4
    c: PointOnObject(g3,g-3)
    c: DistanceX(g4,g0) = 0.5
FEATURE [PartDesign::Groove] Groove235  label="M3 Nut Smooth227"
  Angle = 360
  Axis = (-2e-16,3e-16,1)
  Base = (0,0,0)
  BaseFeature = -> Pad1119
  Profile = -> Sketch2519
  ReferenceAxis = -> Sketch2519 [V_Axis]
  Reversed = true
FEATURE [PartDesign::Chamfer] Chamfer565  label="M3 Nut Smooth Hole227"
  Base = -> Groove235 [Edge24,Edge23]
  BaseFeature = -> Groove235
  Size = 0.2
FEATURE [PartDesign::Body] Body726  label="M3 Nut126"
  Group = -> [Sketch2509,Pad1119,Sketch2519,Groove235,Chamfer565]
  Origin = -> Origin1069
  Placement = pos=(29,-1.5,0) rot=(0,0,-1;1.5708rad)
  Tip = -> Chamfer565
FEATURE [App::Part] Part300  label="Nuts Cameramount"
  Group = -> [Body726,Body731,Body733,Body732]
  Origin = -> Origin1066
  Placement = pos=(14,-9.27342,80.9055) rot=(1,0,0;0.426558rad)
FEATURE [Sketcher::SketchObject] Sketch2523
  MapMode = 5
  Support = -> [XY_Plane1073]
  sketch-geometry (1):
    g0: Circle CenterX=0 CenterY=0 CenterZ=0 NormalX=0 NormalY=0 NormalZ=1 AngleXU=0 Radius=2.75
  constraints (2):
    c: Coincident(g0,g-1)
    c: Radius(g0) = 2.75
FEATURE [PartDesign::Pad] Pad1133  label="M3x8 Head177"
  Length = 3
  Length2 = 100
  Profile = -> Sketch2523
  Type = 0
FEATURE [Sketcher::SketchObject] Sketch2524
  MapMode = 5
  Support = -> [XY_Plane1066]
  sketch-geometry (1):
    g0: Circle CenterX=0 CenterY=0 CenterZ=0 NormalX=0 NormalY=0 NormalZ=1 AngleXU=0 Radius=2.75
  constraints (2):
    c: Coincident(g0,g-1)
    c: Radius(g0) = 2.75
FEATURE [PartDesign::Pad] Pad1126  label="M3x8 Head172"
  Length = 3
  Length2 = 100
  Profile = -> Sketch2524
  Type = 0
FEATURE [Sketcher::SketchObject] Sketch2525
  MapMode = 5
  Placement = pos=(0,0,3) rot=(0,0,1;0rad)
  Support = -> [Pad1133]
  sketch-geometry (1):
    g0: Circle CenterX=0 CenterY=0 CenterZ=0 NormalX=0 NormalY=0 NormalZ=1 AngleXU=0 Radius=1.5
  constraints (2):
    c: Coincident(g0,g-1)
    c: Radius(g0) = 1.5
FEATURE [PartDesign::Pad] Pad1125  label="M3x8 Thread173"
  BaseFeature = -> Pad1133
  Length = 8
  Length2 = 100
  Profile = -> Sketch2525
  Type = 0
FEATURE [Sketcher::SketchObject] Sketch2522
  MapMode = 5
  Placement = pos=(0,0,0) rot=(1,0,0;3.14159rad)
  Support = -> [Pad1125]
  sketch-geometry (7):
    g0: LineSegment StartX=1.275 StartY=0.736122 StartZ=0 EndX=0 EndY=1.47224 EndZ=0
    g1: LineSegment StartX=0 StartY=1.47224 StartZ=0 EndX=-1.275 EndY=0.736122 EndZ=0
    g2: LineSegment StartX=-1.275 StartY=0.736122 StartZ=0 EndX=-1.275 EndY=-0.736122 EndZ=0
    g3: LineSegment StartX=-1.275 StartY=-0.736122 StartZ=0 EndX=1.34766e-11 EndY=-1.47224 EndZ=0
    g4: LineSegment StartX=1.34766e-11 StartY=-1.47224 StartZ=0 EndX=1.275 EndY=-0.736122 EndZ=0
    g5: LineSegment StartX=1.275 StartY=-0.736122 StartZ=0 EndX=1.275 EndY=0.736122 EndZ=0
    g6: Circle [constr] CenterX=0 CenterY=0 CenterZ=0 NormalX=0 NormalY=0 NormalZ=1 AngleXU=0 Radius=1.47224
  constraints (16):
    c: Coincident(g0,g1)
    c: Coincident(g1,g2)
    c: Coincident(g2,g3)
    c: Coincident(g3,g4)
    c: Coincident(g4,g5)
    c: Coincident(g5,g0)
    c: Equal(g0, g1-g5) x5
    c: PointOnObject(g0,g6)
    c: PointOnObject(g1,g6)
    c: PointOnObject(g2,g6)
    c: PointOnObject(g3,g6)
    c: PointOnObject(g4,g6)
    c: PointOnObject(g5,g6)
    c: Coincident(g6,g-1)
    c: PointOnObject(g0,g-2)
    c: DistanceX(g1,g0) = 2.55
FEATURE [PartDesign::Pocket] Pocket900  label="M3x8 Wrench174"
  BaseFeature = -> Pad1125
  Length = 1.3
  Length2 = 100
  Profile = -> Sketch2522
  Type = 0
FEATURE [PartDesign::Chamfer] Chamfer566  label="M3x8 Smooth177"
  Base = -> Pocket900 [Face11,Edge2,Edge24,Edge3]
  BaseFeature = -> Pocket900
  Size = 0.2
FEATURE [PartDesign::Body] Body734  label="M3x143"
  Group = -> [Sketch2523,Pad1133,Sketch2525,Pad1125,Sketch2522,Pocket900,Chamfer566]
  Origin = -> Origin1072
  Placement = pos=(42.75,-29.5,0) rot=(0,0,1;0rad)
  Tip = -> Chamfer566
FEATURE [Sketcher::SketchObject] Sketch2527
  MapMode = 5
  Support = -> [XY_Plane1069]
  sketch-geometry (1):
    g0: Circle CenterX=0 CenterY=0 CenterZ=0 NormalX=0 NormalY=0 NormalZ=1 AngleXU=0 Radius=2.75
  constraints (2):
    c: Coincident(g0,g-1)
    c: Radius(g0) = 2.75
FEATURE [PartDesign::Pad] Pad1129  label="M3x8 Head174"
  Length = 3
  Length2 = 100
  Profile = -> Sketch2527
  Type = 0
FEATURE [Sketcher::SketchObject] Sketch2529
  MapMode = 5
  Placement = pos=(0,0,3) rot=(0,0,1;0rad)
  Support = -> [Pad1129]
  sketch-geometry (1):
    g0: Circle CenterX=0 CenterY=0 CenterZ=0 NormalX=0 NormalY=0 NormalZ=1 AngleXU=0 Radius=1.5
  constraints (2):
    c: Coincident(g0,g-1)
    c: Radius(g0) = 1.5
FEATURE [PartDesign::Pad] Pad1122  label="M3x8 Thread171"
  BaseFeature = -> Pad1129
  Length = 8
  Length2 = 100
  Profile = -> Sketch2529
  Type = 0
FEATURE [Sketcher::SketchObject] Sketch2521
  MapMode = 5
  Placement = pos=(0,0,0) rot=(1,0,0;3.14159rad)
  Support = -> [Pad1122]
  sketch-geometry (7):
    g0: LineSegment StartX=1.275 StartY=0.736122 StartZ=0 EndX=0 EndY=1.47224 EndZ=0
    g1: LineSegment StartX=0 StartY=1.47224 StartZ=0 EndX=-1.275 EndY=0.736122 EndZ=0
    g2: LineSegment StartX=-1.275 StartY=0.736122 StartZ=0 EndX=-1.275 EndY=-0.736122 EndZ=0
    g3: LineSegment StartX=-1.275 StartY=-0.736122 StartZ=0 EndX=1.34766e-11 EndY=-1.47224 EndZ=0
    g4: LineSegment StartX=1.34766e-11 StartY=-1.47224 StartZ=0 EndX=1.275 EndY=-0.736122 EndZ=0
    g5: LineSegment StartX=1.275 StartY=-0.736122 StartZ=0 EndX=1.275 EndY=0.736122 EndZ=0
    g6: Circle [constr] CenterX=0 CenterY=0 CenterZ=0 NormalX=0 NormalY=0 NormalZ=1 AngleXU=0 Radius=1.47224
  constraints (16):
    c: Coincident(g0,g1)
    c: Coincident(g1,g2)
    c: Coincident(g2,g3)
    c: Coincident(g3,g4)
    c: Coincident(g4,g5)
    c: Coincident(g5,g0)
    c: Equal(g0, g1-g5) x5
    c: PointOnObject(g0,g6)
    c: PointOnObject(g1,g6)
    c: PointOnObject(g2,g6)
    c: PointOnObject(g3,g6)
    c: PointOnObject(g4,g6)
    c: PointOnObject(g5,g6)
    c: Coincident(g6,g-1)
    c: PointOnObject(g0,g-2)
    c: DistanceX(g1,g0) = 2.55
FEATURE [PartDesign::Pocket] Pocket897  label="M3x8 Wrench171"
  BaseFeature = -> Pad1122
  Length = 1.3
  Length2 = 100
  Profile = -> Sketch2521
  Type = 0
FEATURE [PartDesign::Chamfer] Chamfer547  label="M3x8 Smooth170"
  Base = -> Pocket897 [Face11,Edge2,Edge24,Edge3]
  BaseFeature = -> Pocket897
  Size = 0.2
FEATURE [PartDesign::Body] Body752  label="M3x144"
  Group = -> [Sketch2527,Pad1129,Sketch2529,Pad1122,Sketch2521,Pocket897,Chamfer547]
  Origin = -> Origin1074
  Placement = pos=(42.75,0,0) rot=(0,0,1;0rad)
  Tip = -> Chamfer547
FEATURE [Sketcher::SketchObject] Sketch2530
  MapMode = 5
  Placement = pos=(0,0,3) rot=(0,0,1;0rad)
  Support = -> [Pad1126]
  sketch-geometry (1):
    g0: Circle CenterX=0 CenterY=0 CenterZ=0 NormalX=0 NormalY=0 NormalZ=1 AngleXU=0 Radius=1.5
  constraints (2):
    c: Coincident(g0,g-1)
    c: Radius(g0) = 1.5
FEATURE [PartDesign::Pad] Pad1123  label="M3x8 Thread172"
  BaseFeature = -> Pad1126
  Length = 8
  Length2 = 100
  Profile = -> Sketch2530
  Type = 0
FEATURE [Sketcher::SketchObject] Sketch2528
  MapMode = 5
  Placement = pos=(0,0,0) rot=(1,0,0;3.14159rad)
  Support = -> [Pad1123]
  sketch-geometry (7):
    g0: LineSegment StartX=1.275 StartY=0.736122 StartZ=0 EndX=0 EndY=1.47224 EndZ=0
    g1: LineSegment StartX=0 StartY=1.47224 StartZ=0 EndX=-1.275 EndY=0.736122 EndZ=0
    g2: LineSegment StartX=-1.275 StartY=0.736122 StartZ=0 EndX=-1.275 EndY=-0.736122 EndZ=0
    g3: LineSegment StartX=-1.275 StartY=-0.736122 StartZ=0 EndX=1.34766e-11 EndY=-1.47224 EndZ=0
    g4: LineSegment StartX=1.34766e-11 StartY=-1.47224 StartZ=0 EndX=1.275 EndY=-0.736122 EndZ=0
    g5: LineSegment StartX=1.275 StartY=-0.736122 StartZ=0 EndX=1.275 EndY=0.736122 EndZ=0
    g6: Circle [constr] CenterX=0 CenterY=0 CenterZ=0 NormalX=0 NormalY=0 NormalZ=1 AngleXU=0 Radius=1.47224
  constraints (16):
    c: Coincident(g0,g1)
    c: Coincident(g1,g2)
    c: Coincident(g2,g3)
    c: Coincident(g3,g4)
    c: Coincident(g4,g5)
    c: Coincident(g5,g0)
    c: Equal(g0, g1-g5) x5
    c: PointOnObject(g0,g6)
    c: PointOnObject(g1,g6)
    c: PointOnObject(g2,g6)
    c: PointOnObject(g3,g6)
    c: PointOnObject(g4,g6)
    c: PointOnObject(g5,g6)
    c: Coincident(g6,g-1)
    c: PointOnObject(g0,g-2)
    c: DistanceX(g1,g0) = 2.55
FEATURE [PartDesign::Pocket] Pocket899  label="M3x8 Wrench173"
  BaseFeature = -> Pad1123
  Length = 1.3
  Length2 = 100
  Profile = -> Sketch2528
  Type = 0
FEATURE [PartDesign::Chamfer] Chamfer555  label="M3x8 Smooth173"
  Base = -> Pocket899 [Face11,Edge2,Edge24,Edge3]
  BaseFeature = -> Pocket899
  Size = 0.2
FEATURE [PartDesign::Body] Body753  label="M3x145"
  Group = -> [Sketch2524,Pad1126,Sketch2530,Pad1123,Sketch2528,Pocket899,Chamfer555]
  Origin = -> Origin1082
  Placement = pos=(71.25,0,0) rot=(0,0,1;0rad)
  Tip = -> Chamfer555
FEATURE [Sketcher::SketchObject] Sketch2531
  MapMode = 5
  Support = -> [XY_Plane1070]
  sketch-geometry (1):
    g0: Circle CenterX=0 CenterY=0 CenterZ=0 NormalX=0 NormalY=0 NormalZ=1 AngleXU=0 Radius=2.75
  constraints (2):
    c: Coincident(g0,g-1)
    c: Radius(g0) = 2.75
FEATURE [PartDesign::Pad] Pad1128  label="M3x8 Head173"
  Length = 3
  Length2 = 100
  Profile = -> Sketch2531
  Type = 0
FEATURE [Sketcher::SketchObject] Sketch2520
  MapMode = 5
  Placement = pos=(0,0,3) rot=(0,0,1;0rad)
  Support = -> [Pad1128]
  sketch-geometry (1):
    g0: Circle CenterX=0 CenterY=0 CenterZ=0 NormalX=0 NormalY=0 NormalZ=1 AngleXU=0 Radius=1.5
  constraints (2):
    c: Coincident(g0,g-1)
    c: Radius(g0) = 1.5
FEATURE [PartDesign::Pad] Pad1127  label="M3x8 Thread174"
  BaseFeature = -> Pad1128
  Length = 8
  Length2 = 100
  Profile = -> Sketch2520
  Type = 0
FEATURE [Sketcher::SketchObject] Sketch2526
  MapMode = 5
  Placement = pos=(0,0,0) rot=(1,0,0;3.14159rad)
  Support = -> [Pad1127]
  sketch-geometry (7):
    g0: LineSegment StartX=1.275 StartY=0.736122 StartZ=0 EndX=0 EndY=1.47224 EndZ=0
    g1: LineSegment StartX=0 StartY=1.47224 StartZ=0 EndX=-1.275 EndY=0.736122 EndZ=0
    g2: LineSegment StartX=-1.275 StartY=0.736122 StartZ=0 EndX=-1.275 EndY=-0.736122 EndZ=0
    g3: LineSegment StartX=-1.275 StartY=-0.736122 StartZ=0 EndX=1.34766e-11 EndY=-1.47224 EndZ=0
    g4: LineSegment StartX=1.34766e-11 StartY=-1.47224 StartZ=0 EndX=1.275 EndY=-0.736122 EndZ=0
    g5: LineSegment StartX=1.275 StartY=-0.736122 StartZ=0 EndX=1.275 EndY=0.736122 EndZ=0
    g6: Circle [constr] CenterX=0 CenterY=0 CenterZ=0 NormalX=0 NormalY=0 NormalZ=1 AngleXU=0 Radius=1.47224
  constraints (16):
    c: Coincident(g0,g1)
    c: Coincident(g1,g2)
    c: Coincident(g2,g3)
    c: Coincident(g3,g4)
    c: Coincident(g4,g5)
    c: Coincident(g5,g0)
    c: Equal(g0, g1-g5) x5
    c: PointOnObject(g0,g6)
    c: PointOnObject(g1,g6)
    c: PointOnObject(g2,g6)
    c: PointOnObject(g3,g6)
    c: PointOnObject(g4,g6)
    c: PointOnObject(g5,g6)
    c: Coincident(g6,g-1)
    c: PointOnObject(g0,g-2)
    c: DistanceX(g1,g0) = 2.55
FEATURE [PartDesign::Pocket] Pocket901  label="M3x8 Wrench175"
  BaseFeature = -> Pad1127
  Length = 1.3
  Length2 = 100
  Profile = -> Sketch2526
  Type = 0
FEATURE [PartDesign::Chamfer] Chamfer548  label="M3x8 Smooth171"
  Base = -> Pocket901 [Face11,Edge2,Edge24,Edge3]
  BaseFeature = -> Pocket901
  Size = 0.2
FEATURE [PartDesign::Body] Body754  label="M3x146"
  Group = -> [Sketch2531,Pad1128,Sketch2520,Pad1127,Sketch2526,Pocket901,Chamfer548]
  Origin = -> Origin1075
  Placement = pos=(71.5,-29.5,0) rot=(0,0,1;0rad)
  Tip = -> Chamfer548
FEATURE [App::Part] Part299  label="Screws Cameramount"
  Group = -> [Body752,Body753,Body734,Body754]
  Origin = -> Origin1070
  Placement = pos=(0,-14.1874,88.0169) rot=(1,0,0;3.56815rad)
FEATURE [App::Part] Part293  label="Camermount Assembly"
  Group = -> [Part300,Part299,Part290,Body714]
  Origin = -> Origin1071
FEATURE [Sketcher::SketchObject] Sketch2533
  MapMode = 5
  Support = -> [XY_Plane1056]
  sketch-geometry (4):
    g0: LineSegment StartX=-1.27 StartY=-1.27 StartZ=0 EndX=1.27 EndY=-1.27 EndZ=0
    g1: LineSegment StartX=1.27 StartY=-1.27 StartZ=0 EndX=1.27 EndY=1.27 EndZ=0
    g2: LineSegment StartX=1.27 StartY=1.27 StartZ=0 EndX=-1.27 EndY=1.27 EndZ=0
    g3: LineSegment StartX=-1.27 StartY=1.27 StartZ=0 EndX=-1.27 EndY=-1.27 EndZ=0
  constraints (10):
    c: Coincident(g0,g1)
    c: Coincident(g1,g2)
    c: Coincident(g2,g3)
    c: Coincident(g3,g0)
    c: Horizontal(g0)
    c: Vertical(g3)
    c: Symmetric(g1,g2,g-2)
    c: Symmetric(g0,g1,g-1)
    c: Equal(g3,g2)
    c: DistanceX(g2,g2) = 2.54
FEATURE [PartDesign::Pad] Pad1109
  Length = 2.5
  Length2 = 100
  Profile = -> Sketch2533
  Type = 0
FEATURE [PartDesign::Chamfer] Chamfer553
  Base = -> Pad1109 [Edge2,Edge1,Edge5,Edge8]
  BaseFeature = -> Pad1109
  Size = 0.2
FEATURE [PartDesign::Chamfer] Chamfer552
  Base = -> Chamfer553 [Face5,Face2]
  BaseFeature = -> Chamfer553
  Size = 0.05
FEATURE [PartDesign::Body] Body749  label="Pin Header Block003"
  Group = -> [Sketch2533,Pad1109,Chamfer553,Chamfer552]
  Origin = -> Origin1062
  Tip = -> Chamfer552
FEATURE [Part::FeaturePython] Array005  # Draft array (typed FeaturePython)
  Angle = 360
  ArrayType = 0
  Axis = (0,0,1)
  Base = -> Body749
  Center = (0,0,0)
  Fuse = false
  IntervalAxis = (0,0,0)
  IntervalX = (2.54,0,0)
  IntervalY = (0,1,0)
  IntervalZ = (0,0,1)
  NumberPolar = 1
  NumberX = 4
  NumberY = 1
  NumberZ = 1
FEATURE [Sketcher::SketchObject] Sketch2534
  MapMode = 5
  Support = -> [XY_Plane1036]
  sketch-geometry (8):
    g0: LineSegment StartX=0 StartY=3.17543 StartZ=0 EndX=-2.75 EndY=1.58771 EndZ=0
    g1: LineSegment StartX=-2.75 StartY=1.58771 StartZ=0 EndX=-2.75 EndY=-1.58771 EndZ=0
    g2: LineSegment StartX=-2.75 StartY=-1.58771 StartZ=0 EndX=0 EndY=-3.17543 EndZ=0
    g3: LineSegment StartX=0 StartY=-3.17543 StartZ=0 EndX=2.75 EndY=-1.58771 EndZ=0
    g4: LineSegment StartX=2.75 StartY=-1.58771 StartZ=0 EndX=2.75 EndY=1.58771 EndZ=0
    g5: LineSegment StartX=2.75 StartY=1.58771 StartZ=0 EndX=0 EndY=3.17543 EndZ=0
    g6: Circle [constr] CenterX=0 CenterY=0 CenterZ=0 NormalX=0 NormalY=0 NormalZ=1 AngleXU=0 Radius=3.17543
    g7: Circle CenterX=0 CenterY=0 CenterZ=0 NormalX=0 NormalY=0 NormalZ=1 AngleXU=0 Radius=1.5
  constraints (18):
    c: Coincident(g0,g1)
    c: Coincident(g1,g2)
    c: Coincident(g2,g3)
    c: Coincident(g3,g4)
    c: Coincident(g4,g5)
    c: Coincident(g5,g0)
    c: Equal(g0, g1-g5) x5
    c: PointOnObject(g0,g6)
    c: PointOnObject(g1,g6)
    c: PointOnObject(g2,g6)
    c: PointOnObject(g3,g6)
    c: PointOnObject(g4,g6)
    c: PointOnObject(g5,g6)
    c: Coincident(g6,g-1)
    c: PointOnObject(g5,g-2)
    c: DistanceX(g0,g4) = 5.5
    c: Coincident(g7,g-1)
    c: Radius(g7) = 1.5
FEATURE [PartDesign::Pad] Pad1115  label="M3 Nut Primitive222"
  Length = 1.2
  Length2 = 1.2
  Profile = -> Sketch2534
  Type = 4
FEATURE [Sketcher::SketchObject] Sketch2532
  ExternalGeometry = -> [Pad1115]
  MapMode = 5
  Placement = pos=(0,0,0) rot=(0.57735,0.57735,0.57735;2.0944rad)
  Support = -> [YZ_Plane1029]
  sketch-geometry (6):
    g0: LineSegment StartX=-2.67543 StartY=1.2 StartZ=0 EndX=-3.67543 EndY=1.2 EndZ=0
    g1: LineSegment StartX=-3.67543 StartY=1.2 StartZ=0 EndX=-3.67543 EndY=-1.2 EndZ=0
    g2: LineSegment StartX=-3.67543 StartY=-1.2 StartZ=0 EndX=-2.67543 EndY=-1.2 EndZ=0
    g3: LineSegment StartX=-2.67543 StartY=-1.2 StartZ=0 EndX=-3.17543 EndY=-1 EndZ=0
    g4: LineSegment StartX=-3.17543 StartY=-1 StartZ=0 EndX=-3.17543 EndY=1 EndZ=0
    g5: LineSegment StartX=-3.17543 StartY=1 StartZ=0 EndX=-2.67543 EndY=1.2 EndZ=0
  constraints (15):
    c: Horizontal(g0)
    c: Coincident(g0,g1)
    c: Coincident(g1,g2)
    c: Coincident(g2,g3)
    c: Coincident(g3,g4)
    c: Coincident(g4,g5)
    c: Coincident(g5,g0)
    c: Symmetric(g4,g3,g-1)
    c: Symmetric(g0,g2,g-1)
    c: Symmetric(g1,g0,g-1)
    c: DistanceX(g0,g4) = 0.5
    c: DistanceY(g3,g4) = 2
    c: DistanceY(g1,g0) = 2.4
    c: PointOnObject(g3,g-3)
    c: DistanceX(g4,g0) = 0.5
FEATURE [PartDesign::Groove] Groove232  label="M3 Nut Smooth224"
  Angle = 360
  Axis = (-2e-16,3e-16,1)
  Base = (0,0,0)
  BaseFeature = -> Pad1115
  Profile = -> Sketch2532
  ReferenceAxis = -> Sketch2532 [V_Axis]
  Reversed = true
FEATURE [PartDesign::Chamfer] Chamfer560  label="M3 Nut Smooth Hole224"
  Base = -> Groove232 [Edge24,Edge23]
  BaseFeature = -> Groove232
  Size = 0.2
FEATURE [PartDesign::Body] Body740  label="M3 Nut130"
  Group = -> [Sketch2534,Pad1115,Sketch2532,Groove232,Chamfer560]
  Origin = -> Origin1058
  Tip = -> Chamfer560
FEATURE [App::Part] Part280  label="Nuts Front Cover"
  Group = -> [Body740,Body707,Body751,Body750]
  Origin = -> Origin1063
  Placement = pos=(14,20.45,6.5) rot=(0,0,1;0rad)
FEATURE [App::Part] Part302  label="Front Cover"
  Group = -> [Body713,Part280]
  Origin = -> Origin1076
  Placement = pos=(0,-29,63.75) rot=(0,0,1;0rad)
FEATURE [Sketcher::SketchObject] Sketch2535
  MapMode = 5
  Support = -> [XY_Plane1047]
  sketch-geometry (4):
    g0: ArcOfCircle CenterX=-4 CenterY=7.5 CenterZ=0 NormalX=0 NormalY=0 NormalZ=1 AngleXU=0 Radius=1.5 StartAngle=1.5708 EndAngle=4.71239
    g1: ArcOfCircle CenterX=4 CenterY=7.5 CenterZ=0 NormalX=0 NormalY=0 NormalZ=1 AngleXU=0 Radius=1.5 StartAngle=4.71239 EndAngle=7.85398
    g2: LineSegment StartX=-4 StartY=6 StartZ=0 EndX=4 EndY=6 EndZ=0
    g3: LineSegment StartX=-4 StartY=9 StartZ=0 EndX=4 EndY=9 EndZ=0
  constraints (9):
    c: Tangent(g0,g3) = 1.5708
    c: Tangent(g0,g2) = -1.5708
    c: Tangent(g2,g1) = -1.5708
    c: Tangent(g3,g1) = 1.5708
    c: Horizontal(g2)
    c: Symmetric(g0,g1,g-2)
    c: DistanceX(g0,g1) = 8
    c: Radius(g1) = 1.5
    c: DistanceY(g-1,g0) = 7.5
FEATURE [PartDesign::Pad] Pad1113
  Length = 3
  Length2 = 100
  Profile = -> Sketch2535
  Type = 0
FEATURE [PartDesign::Fillet] Fillet261
  Base = -> Pad1113 [Edge7]
  BaseFeature = -> Pad1113
  Radius = 0.3
FEATURE [PartDesign::Body] Body741  label="HC-SR04 Clock001"
  Group = -> [Sketch2535,Pad1113,Fillet261]
  Origin = -> Origin1035
  Placement = pos=(0,0,2) rot=(0,0,1;0rad)
  Tip = -> Fillet261
FEATURE [Sketcher::SketchObject] Sketch2536
  MapMode = 5
  Support = -> [XY_Plane1049]
  sketch-geometry (4):
    g0: LineSegment StartX=-22.5 StartY=10 StartZ=0 EndX=22.5 EndY=10 EndZ=0
    g1: LineSegment StartX=22.5 StartY=10 StartZ=0 EndX=22.5 EndY=-10 EndZ=0
    g2: LineSegment StartX=22.5 StartY=-10 StartZ=0 EndX=-22.5 EndY=-10 EndZ=0
    g3: LineSegment StartX=-22.5 StartY=-10 StartZ=0 EndX=-22.5 EndY=10 EndZ=0
  constraints (10):
    c: Coincident(g0,g1)
    c: Coincident(g1,g2)
    c: Coincident(g2,g3)
    c: Coincident(g3,g0)
    c: Horizontal(g2)
    c: Vertical(g1)
    c: Symmetric(g0,g0,g-2)
    c: Symmetric(g2,g0,g-1)
    c: DistanceY(g3,g3) = 20
    c: DistanceX(g0,g0) = 45
FEATURE [PartDesign::Pad] Pad1108
  Length = 2
  Length2 = 100
  Profile = -> Sketch2536
  Type = 0
FEATURE [PartDesign::Body] Body744  label="HC-SR04 PCB001"
  Group = -> [Sketch2536,Pad1108]
  Origin = -> Origin1037
  Tip = -> Pad1108
FEATURE [Sketcher::SketchObject] Sketch2537
  MapMode = 5
  Placement = pos=(0,0,0) rot=(1,0,0;1.5708rad)
  Support = -> [XZ_Plane1055]
  sketch-geometry (4):
    g0: LineSegment StartX=-0.32 StartY=-3 StartZ=0 EndX=0.32 EndY=-3 EndZ=0
    g1: LineSegment StartX=0.32 StartY=-3 StartZ=0 EndX=0.32 EndY=8.54 EndZ=0
    g2: LineSegment StartX=0.32 StartY=8.54 StartZ=0 EndX=-0.32 EndY=8.54 EndZ=0
    g3: LineSegment StartX=-0.32 StartY=8.54 StartZ=0 EndX=-0.32 EndY=-3 EndZ=0
  constraints (11):
    c: Coincident(g0,g1)
    c: Coincident(g1,g2)
    c: Coincident(g2,g3)
    c: Coincident(g3,g0)
    c: Horizontal(g0)
    c: Vertical(g1)
    c: Vertical(g3)
    c: DistanceY(g-1,g1) = 8.54
    c: DistanceY(g0,g-1) = 3
    c: Symmetric(g2,g1,g-2)
    c: DistanceX(g2,g2) = 0.64
FEATURE [PartDesign::Pad] Pad1105
  Length = 0.32
  Length2 = 0.32
  Placement = pos=(0,0,0) rot=(1,0,0;1.5708rad)
  Profile = -> Sketch2537
  Type = 4
FEATURE [PartDesign::Chamfer] Chamfer551
  Base = -> Pad1105 [Face3,Face1]
  BaseFeature = -> Pad1105
  Placement = pos=(0,0,0) rot=(1,0,0;1.5708rad)
  Size = 0.16
FEATURE [PartDesign::Body] Body748  label="Pin Header Pin003"
  Group = -> [Sketch2537,Pad1105,Chamfer551]
  Origin = -> Origin1054
  Tip = -> Chamfer551
FEATURE [Part::FeaturePython] Array004  # Draft array (typed FeaturePython)
  Angle = 360
  ArrayType = 0
  Axis = (0,0,1)
  Base = -> Body748
  Center = (0,0,0)
  Fuse = false
  IntervalAxis = (0,0,0)
  IntervalX = (2.54,0,0)
  IntervalY = (0,1,0)
  IntervalZ = (0,0,1)
  NumberPolar = 1
  NumberX = 4
  NumberY = 1
  NumberZ = 1
FEATURE [App::Part] Part284  label="Pin Header003"
  Group = -> [Body749,Body748,Array005,Array004]
  Origin = -> Origin1049
  Placement = pos=(3.8,-8.4,5e-16) rot=(0,1,0;3.14159rad)
FEATURE [Sketcher::SketchObject] Sketch2538
  MapMode = 5
  Support = -> [XY_Plane1058]
  sketch-geometry (1):
    g0: Circle CenterX=-13 CenterY=0 CenterZ=0 NormalX=0 NormalY=0 NormalZ=1 AngleXU=0 Radius=8
  constraints (3):
    c: PointOnObject(g0,g-1)
    c: Radius(g0) = 8
    c: DistanceX(g0,g-1) = 13
FEATURE [PartDesign::Pad] Pad1099
  Length = 12
  Length2 = 100
  Profile = -> Sketch2538
  Type = 0
FEATURE [PartDesign::Fillet] Fillet262
  Base = -> Pad1099 [Edge3]
  BaseFeature = -> Pad1099
  Radius = 0.3
FEATURE [PartDesign::Body] Body745  label="HC-SR04 Trigger Base"
  Group = -> [Sketch2538,Pad1099,Fillet262]
  Origin = -> Origin1046
  Placement = pos=(0,0,2) rot=(0,0,1;0rad)
  Tip = -> Fillet262
FEATURE [Sketcher::SketchObject] Sketch2539
  AttachmentOffset = pos=(0,0,14) rot=(0,0,1;0rad)
  MapMode = 5
  Placement = pos=(0,0,14) rot=(0,0,1;0rad)
  Support = -> [XY_Plane1013]
  sketch-geometry (1):
    g0: Circle CenterX=13 CenterY=0 CenterZ=0 NormalX=0 NormalY=0 NormalZ=1 AngleXU=0 Radius=6
  constraints (3):
    c: PointOnObject(g0,g-1)
    c: Radius(g0) = 6
    c: DistanceX(g-1,g0) = 13
FEATURE [PartDesign::Pad] Pad1100
  Length = 0.1
  Length2 = 100
  Profile = -> Sketch2539
  Type = 0
FEATURE [PartDesign::Body] Body710  label="HC-SR04 Echo Cap001"
  Group = -> [Sketch2539,Pad1100]
  Origin = -> Origin1042
  Tip = -> Pad1100
FEATURE [Sketcher::SketchObject] Sketch2540
  AttachmentOffset = pos=(0,0,14) rot=(0,0,1;0rad)
  MapMode = 5
  Placement = pos=(0,0,14) rot=(0,0,1;0rad)
  Support = -> [XY_Plane1055]
  sketch-geometry (1):
    g0: Circle CenterX=-13 CenterY=0 CenterZ=0 NormalX=0 NormalY=0 NormalZ=1 AngleXU=0 Radius=6
  constraints (3):
    c: PointOnObject(g0,g-1)
    c: DistanceX(g0,g-1) = 13
    c: Radius(g0) = 6
FEATURE [PartDesign::Pad] Pad1110
  Length = 0.1
  Length2 = 100
  Profile = -> Sketch2540
  Type = 0
FEATURE [PartDesign::Body] Body747  label="HC-SR04 Trigger Cap"
  Group = -> [Sketch2540,Pad1110]
  Origin = -> Origin1036
  Tip = -> Pad1110
FEATURE [App::Part] Part286  label="HC-SR04 Trigger"
  Group = -> [Body745,Body747]
  Origin = -> Origin1059
FEATURE [Sketcher::SketchObject] Sketch2541
  MapMode = 5
  Support = -> [XY_Plane1011]
  sketch-geometry (1):
    g0: Circle CenterX=13 CenterY=0 CenterZ=0 NormalX=0 NormalY=0 NormalZ=1 AngleXU=0 Radius=8
  constraints (3):
    c: PointOnObject(g0,g-1)
    c: Radius(g0) = 8
    c: DistanceX(g-1,g0) = 13
FEATURE [PartDesign::Pad] Pad1102
  Length = 12
  Length2 = 100
  Profile = -> Sketch2541
  Type = 0
FEATURE [PartDesign::Fillet] Fillet259
  Base = -> Pad1102 [Edge3]
  BaseFeature = -> Pad1102
  Radius = 0.3
FEATURE [PartDesign::Body] Body708  label="HC-SR04 Echo Base001"
  Group = -> [Sketch2541,Pad1102,Fillet259]
  Origin = -> Origin1039
  Placement = pos=(0,0,2) rot=(0,0,1;0rad)
  Tip = -> Fillet259
FEATURE [App::Part] Part279  label="HC-SR04 Echo001"
  Group = -> [Body708,Body710]
  Origin = -> Origin1060
FEATURE [Sketcher::SketchObject] Sketch2542
  AttachmentOffset = pos=(0,0,14) rot=(0,0,1;0rad)
  MapMode = 5
  Placement = pos=(0,0,14) rot=(0,0,1;0rad)
  Support = -> [XY_Plane1061]
  sketch-geometry (1):
    g0: Circle CenterX=13 CenterY=0 CenterZ=0 NormalX=0 NormalY=0 NormalZ=1 AngleXU=0 Radius=6
  constraints (3):
    c: PointOnObject(g0,g-1)
    c: Radius(g0) = 6
    c: DistanceX(g-1,g0) = 13
FEATURE [PartDesign::Pad] Pad072
  Length = 0.1
  Length2 = 100
  Profile = -> Sketch2542
  Type = 0
FEATURE [PartDesign::Body] Body742  label="HC-SR04 Echo Cap"
  Group = -> [Sketch2542,Pad072]
  Origin = -> Origin1041
  Tip = -> Pad072
FEATURE [Sketcher::SketchObject] Sketch2543
  MapMode = 5
  Support = -> [XY_Plane1059]
  sketch-geometry (1):
    g0: Circle CenterX=13 CenterY=0 CenterZ=0 NormalX=0 NormalY=0 NormalZ=1 AngleXU=0 Radius=8
  constraints (3):
    c: PointOnObject(g0,g-1)
    c: Radius(g0) = 8
    c: DistanceX(g-1,g0) = 13
FEATURE [PartDesign::Pad] Pad1111
  Length = 12
  Length2 = 100
  Profile = -> Sketch2543
  Type = 0
FEATURE [PartDesign::Fillet] Fillet263
  Base = -> Pad1111 [Edge3]
  BaseFeature = -> Pad1111
  Radius = 0.3
FEATURE [PartDesign::Body] Body743  label="HC-SR04 Echo Base"
  Group = -> [Sketch2543,Pad1111,Fillet263]
  Origin = -> Origin1043
  Placement = pos=(0,0,2) rot=(0,0,1;0rad)
  Tip = -> Fillet263
FEATURE [App::Part] Part289  label="HC-SR04 Echo"
  Group = -> [Body743,Body742]
  Origin = -> Origin1050
FEATURE [App::Part] Part298  label="HC-SR04 (left side)"
  Group = -> [Body725,Body727,Part295,Part286,Part289]
  Origin = -> Origin1044
  Placement = pos=(85.2137,6.9,78.4031) rot=(0.704063,0.704063,-0.092692;3.32645rad)
FEATURE [Sketcher::SketchObject] Sketch2544
  MapMode = 5
  Support = -> [XY_Plane1012]
  sketch-geometry (1):
    g0: Circle CenterX=-13 CenterY=0 CenterZ=0 NormalX=0 NormalY=0 NormalZ=1 AngleXU=0 Radius=8
  constraints (3):
    c: PointOnObject(g0,g-1)
    c: Radius(g0) = 8
    c: DistanceX(g0,g-1) = 13
FEATURE [PartDesign::Pad] Pad1112
  Length = 12
  Length2 = 100
  Profile = -> Sketch2544
  Type = 0
FEATURE [PartDesign::Fillet] Fillet260
  Base = -> Pad1112 [Edge3]
  BaseFeature = -> Pad1112
  Radius = 0.3
FEATURE [PartDesign::Body] Body709  label="HC-SR04 Trigger Base001"
  Group = -> [Sketch2544,Pad1112,Fillet260]
  Origin = -> Origin1038
  Placement = pos=(0,0,2) rot=(0,0,1;0rad)
  Tip = -> Fillet260
FEATURE [Sketcher::SketchObject] Sketch2545
  AttachmentOffset = pos=(0,0,14) rot=(0,0,1;0rad)
  MapMode = 5
  Placement = pos=(0,0,14) rot=(0,0,1;0rad)
  Support = -> [XY_Plane1010]
  sketch-geometry (1):
    g0: Circle CenterX=-13 CenterY=0 CenterZ=0 NormalX=0 NormalY=0 NormalZ=1 AngleXU=0 Radius=6
  constraints (3):
    c: PointOnObject(g0,g-1)
    c: DistanceX(g0,g-1) = 13
    c: Radius(g0) = 6
FEATURE [PartDesign::Pad] Pad1101
  Length = 0.1
  Length2 = 100
  Profile = -> Sketch2545
  Type = 0
FEATURE [PartDesign::Body] Body711  label="HC-SR04 Trigger Cap001"
  Group = -> [Sketch2545,Pad1101]
  Origin = -> Origin1051
  Tip = -> Pad1101
FEATURE [App::Part] Part278  label="HC-SR04 Trigger001"
  Group = -> [Body709,Body711]
  Origin = -> Origin1053
FEATURE [App::Part] Part288  label="HC-SR04 (right side)"
  Group = -> [Body744,Body741,Part284,Part278,Part279]
  Origin = -> Origin1052
  Placement = pos=(29.0516,6.9,78.4604) rot=(-0.704063,0.704063,-0.092692;2.95674rad)
FEATURE [PartDesign::Body] Body757  label="M3x149"
  Group = -> [Sketch2459,Pad1136,Sketch2463,Pad1137,Sketch2458,Pocket904,Chamfer563]
  Origin = -> Origin1080
  Placement = pos=(100,-48.5,0) rot=(0,0,1;0rad)
  Tip = -> Chamfer563
FEATURE [PartDesign::Body] Body758  label="M3x150"
  Group = -> [Sketch2452,Pad1124,Sketch2455,Pad1131,Sketch2454,Pocket898,Chamfer557]
  Origin = -> Origin1078
  Placement = pos=(14,-20.5,0) rot=(0,0,1;0rad)
  Tip = -> Chamfer557
FEATURE [App::Part] Part301  label="Front Cover Screws"
  Group = -> [Body758,Body755,Body756,Body757]
  Origin = -> Origin1079
  Placement = pos=(0,-29,79) rot=(-1,0,0;3.14159rad)
FEATURE [App::Part] Part282  label="Head"
  Group = -> [Part298,Part288,Part292,Part293,Part302,Part301]
  Origin = -> Origin1067
  Placement = pos=(112.929,-42.5,164.462) rot=(-0.476092,0.476092,0.739373;4.41492rad)
FEATURE [Sketcher::SketchObject] Sketch2546
  MapMode = 5
  Support = -> [XY_Plane1082]
  sketch-geometry (8):
    g0: LineSegment StartX=0 StartY=3.17543 StartZ=0 EndX=-2.75 EndY=1.58771 EndZ=0
    g1: LineSegment StartX=-2.75 StartY=1.58771 StartZ=0 EndX=-2.75 EndY=-1.58771 EndZ=0
    g2: LineSegment StartX=-2.75 StartY=-1.58771 StartZ=0 EndX=0 EndY=-3.17543 EndZ=0
    g3: LineSegment StartX=0 StartY=-3.17543 StartZ=0 EndX=2.75 EndY=-1.58771 EndZ=0
    g4: LineSegment StartX=2.75 StartY=-1.58771 StartZ=0 EndX=2.75 EndY=1.58771 EndZ=0
    g5: LineSegment StartX=2.75 StartY=1.58771 StartZ=0 EndX=0 EndY=3.17543 EndZ=0
    g6: Circle [constr] CenterX=0 CenterY=0 CenterZ=0 NormalX=0 NormalY=0 NormalZ=1 AngleXU=0 Radius=3.17543
    g7: Circle CenterX=0 CenterY=0 CenterZ=0 NormalX=0 NormalY=0 NormalZ=1 AngleXU=0 Radius=1.5
  constraints (18):
    c: Coincident(g0,g1)
    c: Coincident(g1,g2)
    c: Coincident(g2,g3)
    c: Coincident(g3,g4)
    c: Coincident(g4,g5)
    c: Coincident(g5,g0)
    c: Equal(g0, g1-g5) x5
    c: PointOnObject(g0,g6)
    c: PointOnObject(g1,g6)
    c: PointOnObject(g2,g6)
    c: PointOnObject(g3,g6)
    c: PointOnObject(g4,g6)
    c: PointOnObject(g5,g6)
    c: Coincident(g6,g-1)
    c: PointOnObject(g5,g-2)
    c: DistanceX(g0,g4) = 5.5
    c: Coincident(g7,g-1)
    c: Radius(g7) = 1.5
FEATURE [PartDesign::Pad] Pad1138  label="M3 Nut Primitive229"
  Length = 1.2
  Length2 = 1.2
  Profile = -> Sketch2546
  Type = 4
FEATURE [Sketcher::SketchObject] Sketch2547
  ExternalGeometry = -> [Pad1138]
  MapMode = 5
  Placement = pos=(0,0,0) rot=(0.57735,0.57735,0.57735;2.0944rad)
  Support = -> [YZ_Plane1076]
  sketch-geometry (6):
    g0: LineSegment StartX=-2.67543 StartY=1.2 StartZ=0 EndX=-3.67543 EndY=1.2 EndZ=0
    g1: LineSegment StartX=-3.67543 StartY=1.2 StartZ=0 EndX=-3.67543 EndY=-1.2 EndZ=0
    g2: LineSegment StartX=-3.67543 StartY=-1.2 StartZ=0 EndX=-2.67543 EndY=-1.2 EndZ=0
    g3: LineSegment StartX=-2.67543 StartY=-1.2 StartZ=0 EndX=-3.17543 EndY=-1 EndZ=0
    g4: LineSegment StartX=-3.17543 StartY=-1 StartZ=0 EndX=-3.17543 EndY=1 EndZ=0
    g5: LineSegment StartX=-3.17543 StartY=1 StartZ=0 EndX=-2.67543 EndY=1.2 EndZ=0
  constraints (15):
    c: Horizontal(g0)
    c: Coincident(g0,g1)
    c: Coincident(g1,g2)
    c: Coincident(g2,g3)
    c: Coincident(g3,g4)
    c: Coincident(g4,g5)
    c: Coincident(g5,g0)
    c: Symmetric(g4,g3,g-1)
    c: Symmetric(g0,g2,g-1)
    c: Symmetric(g1,g0,g-1)
    c: DistanceX(g0,g4) = 0.5
    c: DistanceY(g3,g4) = 2
    c: DistanceY(g1,g0) = 2.4
    c: PointOnObject(g3,g-3)
    c: DistanceX(g4,g0) = 0.5
FEATURE [PartDesign::Groove] Groove237  label="M3 Nut Smooth229"
  Angle = 360
  Axis = (-2e-16,3e-16,1)
  Base = (0,0,0)
  BaseFeature = -> Pad1138
  Profile = -> Sketch2547
  ReferenceAxis = -> Sketch2547 [V_Axis]
  Reversed = true
FEATURE [PartDesign::Chamfer] Chamfer571  label="M3 Nut Smooth Hole229"
  Base = -> Groove237 [Edge24,Edge23]
  BaseFeature = -> Groove237
  Size = 0.2
FEATURE [PartDesign::Body] Body759  label="M3 Nut133"
  Group = -> [Sketch2546,Pad1138,Sketch2547,Groove237,Chamfer571]
  Origin = -> Origin1084
  Tip = -> Chamfer571
FEATURE [Sketcher::SketchObject] Sketch2548
  MapMode = 5
  Support = -> [XY_Plane1083]
  sketch-geometry (8):
    g0: LineSegment StartX=0 StartY=3.17543 StartZ=0 EndX=-2.75 EndY=1.58771 EndZ=0
    g1: LineSegment StartX=-2.75 StartY=1.58771 StartZ=0 EndX=-2.75 EndY=-1.58771 EndZ=0
    g2: LineSegment StartX=-2.75 StartY=-1.58771 StartZ=0 EndX=0 EndY=-3.17543 EndZ=0
    g3: LineSegment StartX=0 StartY=-3.17543 StartZ=0 EndX=2.75 EndY=-1.58771 EndZ=0
    g4: LineSegment StartX=2.75 StartY=-1.58771 StartZ=0 EndX=2.75 EndY=1.58771 EndZ=0
    g5: LineSegment StartX=2.75 StartY=1.58771 StartZ=0 EndX=0 EndY=3.17543 EndZ=0
    g6: Circle [constr] CenterX=0 CenterY=0 CenterZ=0 NormalX=0 NormalY=0 NormalZ=1 AngleXU=0 Radius=3.17543
    g7: Circle CenterX=0 CenterY=0 CenterZ=0 NormalX=0 NormalY=0 NormalZ=1 AngleXU=0 Radius=1.5
  constraints (18):
    c: Coincident(g0,g1)
    c: Coincident(g1,g2)
    c: Coincident(g2,g3)
    c: Coincident(g3,g4)
    c: Coincident(g4,g5)
    c: Coincident(g5,g0)
    c: Equal(g0, g1-g5) x5
    c: PointOnObject(g0,g6)
    c: PointOnObject(g1,g6)
    c: PointOnObject(g2,g6)
    c: PointOnObject(g3,g6)
    c: PointOnObject(g4,g6)
    c: PointOnObject(g5,g6)
    c: Coincident(g6,g-1)
    c: PointOnObject(g5,g-2)
    c: DistanceX(g0,g4) = 5.5
    c: Coincident(g7,g-1)
    c: Radius(g7) = 1.5
FEATURE [PartDesign::Pad] Pad1139  label="M3 Nut Primitive230"
  Length = 1.2
  Length2 = 1.2
  Profile = -> Sketch2548
  Type = 4
FEATURE [Sketcher::SketchObject] Sketch2549
  ExternalGeometry = -> [Pad1139]
  MapMode = 5
  Placement = pos=(0,0,0) rot=(0.57735,0.57735,0.57735;2.0944rad)
  Support = -> [YZ_Plane1077]
  sketch-geometry (6):
    g0: LineSegment StartX=-2.67543 StartY=1.2 StartZ=0 EndX=-3.67543 EndY=1.2 EndZ=0
    g1: LineSegment StartX=-3.67543 StartY=1.2 StartZ=0 EndX=-3.67543 EndY=-1.2 EndZ=0
    g2: LineSegment StartX=-3.67543 StartY=-1.2 StartZ=0 EndX=-2.67543 EndY=-1.2 EndZ=0
    g3: LineSegment StartX=-2.67543 StartY=-1.2 StartZ=0 EndX=-3.17543 EndY=-1 EndZ=0
    g4: LineSegment StartX=-3.17543 StartY=-1 StartZ=0 EndX=-3.17543 EndY=1 EndZ=0
    g5: LineSegment StartX=-3.17543 StartY=1 StartZ=0 EndX=-2.67543 EndY=1.2 EndZ=0
  constraints (15):
    c: Horizontal(g0)
    c: Coincident(g0,g1)
    c: Coincident(g1,g2)
    c: Coincident(g2,g3)
    c: Coincident(g3,g4)
    c: Coincident(g4,g5)
    c: Coincident(g5,g0)
    c: Symmetric(g4,g3,g-1)
    c: Symmetric(g0,g2,g-1)
    c: Symmetric(g1,g0,g-1)
    c: DistanceX(g0,g4) = 0.5
    c: DistanceY(g3,g4) = 2
    c: DistanceY(g1,g0) = 2.4
    c: PointOnObject(g3,g-3)
    c: DistanceX(g4,g0) = 0.5
FEATURE [PartDesign::Groove] Groove238  label="M3 Nut Smooth230"
  Angle = 360
  Axis = (-2e-16,3e-16,1)
  Base = (0,0,0)
  BaseFeature = -> Pad1139
  Profile = -> Sketch2549
  ReferenceAxis = -> Sketch2549 [V_Axis]
  Reversed = true
FEATURE [PartDesign::Chamfer] Chamfer572  label="M3 Nut Smooth Hole230"
  Base = -> Groove238 [Edge24,Edge23]
  BaseFeature = -> Groove238
  Size = 0.2
FEATURE [PartDesign::Body] Body760  label="M3 Nut134"
  Group = -> [Sketch2548,Pad1139,Sketch2549,Groove238,Chamfer572]
  Origin = -> Origin1085
  Placement = pos=(0,10,0) rot=(0,0,1;0rad)
  Tip = -> Chamfer572
FEATURE [Sketcher::SketchObject] Sketch2550
  MapMode = 5
  Support = -> [XY_Plane1084]
  sketch-geometry (8):
    g0: LineSegment StartX=0 StartY=3.17543 StartZ=0 EndX=-2.75 EndY=1.58771 EndZ=0
    g1: LineSegment StartX=-2.75 StartY=1.58771 StartZ=0 EndX=-2.75 EndY=-1.58771 EndZ=0
    g2: LineSegment StartX=-2.75 StartY=-1.58771 StartZ=0 EndX=0 EndY=-3.17543 EndZ=0
    g3: LineSegment StartX=0 StartY=-3.17543 StartZ=0 EndX=2.75 EndY=-1.58771 EndZ=0
    g4: LineSegment StartX=2.75 StartY=-1.58771 StartZ=0 EndX=2.75 EndY=1.58771 EndZ=0
    g5: LineSegment StartX=2.75 StartY=1.58771 StartZ=0 EndX=0 EndY=3.17543 EndZ=0
    g6: Circle [constr] CenterX=0 CenterY=0 CenterZ=0 NormalX=0 NormalY=0 NormalZ=1 AngleXU=0 Radius=3.17543
    g7: Circle CenterX=0 CenterY=0 CenterZ=0 NormalX=0 NormalY=0 NormalZ=1 AngleXU=0 Radius=1.5
  constraints (18):
    c: Coincident(g0,g1)
    c: Coincident(g1,g2)
    c: Coincident(g2,g3)
    c: Coincident(g3,g4)
    c: Coincident(g4,g5)
    c: Coincident(g5,g0)
    c: Equal(g0, g1-g5) x5
    c: PointOnObject(g0,g6)
    c: PointOnObject(g1,g6)
    c: PointOnObject(g2,g6)
    c: PointOnObject(g3,g6)
    c: PointOnObject(g4,g6)
    c: PointOnObject(g5,g6)
    c: Coincident(g6,g-1)
    c: PointOnObject(g5,g-2)
    c: DistanceX(g0,g4) = 5.5
    c: Coincident(g7,g-1)
    c: Radius(g7) = 1.5
FEATURE [PartDesign::Pad] Pad1140  label="M3 Nut Primitive231"
  Length = 1.2
  Length2 = 1.2
  Profile = -> Sketch2550
  Type = 4
FEATURE [Sketcher::SketchObject] Sketch2551
  ExternalGeometry = -> [Pad1140]
  MapMode = 5
  Placement = pos=(0,0,0) rot=(0.57735,0.57735,0.57735;2.0944rad)
  Support = -> [YZ_Plane1078]
  sketch-geometry (6):
    g0: LineSegment StartX=-2.67543 StartY=1.2 StartZ=0 EndX=-3.67543 EndY=1.2 EndZ=0
    g1: LineSegment StartX=-3.67543 StartY=1.2 StartZ=0 EndX=-3.67543 EndY=-1.2 EndZ=0
    g2: LineSegment StartX=-3.67543 StartY=-1.2 StartZ=0 EndX=-2.67543 EndY=-1.2 EndZ=0
    g3: LineSegment StartX=-2.67543 StartY=-1.2 StartZ=0 EndX=-3.17543 EndY=-1 EndZ=0
    g4: LineSegment StartX=-3.17543 StartY=-1 StartZ=0 EndX=-3.17543 EndY=1 EndZ=0
    g5: LineSegment StartX=-3.17543 StartY=1 StartZ=0 EndX=-2.67543 EndY=1.2 EndZ=0
  constraints (15):
    c: Horizontal(g0)
    c: Coincident(g0,g1)
    c: Coincident(g1,g2)
    c: Coincident(g2,g3)
    c: Coincident(g3,g4)
    c: Coincident(g4,g5)
    c: Coincident(g5,g0)
    c: Symmetric(g4,g3,g-1)
    c: Symmetric(g0,g2,g-1)
    c: Symmetric(g1,g0,g-1)
    c: DistanceX(g0,g4) = 0.5
    c: DistanceY(g3,g4) = 2
    c: DistanceY(g1,g0) = 2.4
    c: PointOnObject(g3,g-3)
    c: DistanceX(g4,g0) = 0.5
FEATURE [PartDesign::Groove] Groove239  label="M3 Nut Smooth231"
  Angle = 360
  Axis = (-2e-16,3e-16,1)
  Base = (0,0,0)
  BaseFeature = -> Pad1140
  Profile = -> Sketch2551
  ReferenceAxis = -> Sketch2551 [V_Axis]
  Reversed = true
FEATURE [PartDesign::Chamfer] Chamfer573  label="M3 Nut Smooth Hole231"
  Base = -> Groove239 [Edge24,Edge23]
  BaseFeature = -> Groove239
  Size = 0.2
FEATURE [PartDesign::Body] Body761  label="M3 Nut135"
  Group = -> [Sketch2550,Pad1140,Sketch2551,Groove239,Chamfer573]
  Origin = -> Origin1086
  Placement = pos=(10,0,0) rot=(0,0,1;0rad)
  Tip = -> Chamfer573
FEATURE [Sketcher::SketchObject] Sketch2552
  MapMode = 5
  Support = -> [XY_Plane1085]
  sketch-geometry (8):
    g0: LineSegment StartX=0 StartY=3.17543 StartZ=0 EndX=-2.75 EndY=1.58771 EndZ=0
    g1: LineSegment StartX=-2.75 StartY=1.58771 StartZ=0 EndX=-2.75 EndY=-1.58771 EndZ=0
    g2: LineSegment StartX=-2.75 StartY=-1.58771 StartZ=0 EndX=0 EndY=-3.17543 EndZ=0
    g3: LineSegment StartX=0 StartY=-3.17543 StartZ=0 EndX=2.75 EndY=-1.58771 EndZ=0
    g4: LineSegment StartX=2.75 StartY=-1.58771 StartZ=0 EndX=2.75 EndY=1.58771 EndZ=0
    g5: LineSegment StartX=2.75 StartY=1.58771 StartZ=0 EndX=0 EndY=3.17543 EndZ=0
    g6: Circle [constr] CenterX=0 CenterY=0 CenterZ=0 NormalX=0 NormalY=0 NormalZ=1 AngleXU=0 Radius=3.17543
    g7: Circle CenterX=0 CenterY=0 CenterZ=0 NormalX=0 NormalY=0 NormalZ=1 AngleXU=0 Radius=1.5
  constraints (18):
    c: Coincident(g0,g1)
    c: Coincident(g1,g2)
    c: Coincident(g2,g3)
    c: Coincident(g3,g4)
    c: Coincident(g4,g5)
    c: Coincident(g5,g0)
    c: Equal(g0, g1-g5) x5
    c: PointOnObject(g0,g6)
    c: PointOnObject(g1,g6)
    c: PointOnObject(g2,g6)
    c: PointOnObject(g3,g6)
    c: PointOnObject(g4,g6)
    c: PointOnObject(g5,g6)
    c: Coincident(g6,g-1)
    c: PointOnObject(g5,g-2)
    c: DistanceX(g0,g4) = 5.5
    c: Coincident(g7,g-1)
    c: Radius(g7) = 1.5
FEATURE [PartDesign::Pad] Pad1141  label="M3 Nut Primitive232"
  Length = 1.2
  Length2 = 1.2
  Profile = -> Sketch2552
  Type = 4
FEATURE [Sketcher::SketchObject] Sketch2553
  ExternalGeometry = -> [Pad1141]
  MapMode = 5
  Placement = pos=(0,0,0) rot=(0.57735,0.57735,0.57735;2.0944rad)
  Support = -> [YZ_Plane1079]
  sketch-geometry (6):
    g0: LineSegment StartX=-2.67543 StartY=1.2 StartZ=0 EndX=-3.67543 EndY=1.2 EndZ=0
    g1: LineSegment StartX=-3.67543 StartY=1.2 StartZ=0 EndX=-3.67543 EndY=-1.2 EndZ=0
    g2: LineSegment StartX=-3.67543 StartY=-1.2 StartZ=0 EndX=-2.67543 EndY=-1.2 EndZ=0
    g3: LineSegment StartX=-2.67543 StartY=-1.2 StartZ=0 EndX=-3.17543 EndY=-1 EndZ=0
    g4: LineSegment StartX=-3.17543 StartY=-1 StartZ=0 EndX=-3.17543 EndY=1 EndZ=0
    g5: LineSegment StartX=-3.17543 StartY=1 StartZ=0 EndX=-2.67543 EndY=1.2 EndZ=0
  constraints (15):
    c: Horizontal(g0)
    c: Coincident(g0,g1)
    c: Coincident(g1,g2)
    c: Coincident(g2,g3)
    c: Coincident(g3,g4)
    c: Coincident(g4,g5)
    c: Coincident(g5,g0)
    c: Symmetric(g4,g3,g-1)
    c: Symmetric(g0,g2,g-1)
    c: Symmetric(g1,g0,g-1)
    c: DistanceX(g0,g4) = 0.5
    c: DistanceY(g3,g4) = 2
    c: DistanceY(g1,g0) = 2.4
    c: PointOnObject(g3,g-3)
    c: DistanceX(g4,g0) = 0.5
FEATURE [PartDesign::Groove] Groove240  label="M3 Nut Smooth232"
  Angle = 360
  Axis = (-2e-16,3e-16,1)
  Base = (0,0,0)
  BaseFeature = -> Pad1141
  Profile = -> Sketch2553
  ReferenceAxis = -> Sketch2553 [V_Axis]
  Reversed = true
FEATURE [PartDesign::Chamfer] Chamfer574  label="M3 Nut Smooth Hole232"
  Base = -> Groove240 [Edge24,Edge23]
  BaseFeature = -> Groove240
  Size = 0.2
FEATURE [PartDesign::Body] Body762  label="M3 Nut136"
  Group = -> [Sketch2552,Pad1141,Sketch2553,Groove240,Chamfer574]
  Origin = -> Origin1087
  Placement = pos=(10,10,0) rot=(0,0,1;0rad)
  Tip = -> Chamfer574
FEATURE [Sketcher::SketchObject] Sketch2554
  MapMode = 5
  Support = -> [XY_Plane1086]
  sketch-geometry (8):
    g0: LineSegment StartX=0 StartY=3.17543 StartZ=0 EndX=-2.75 EndY=1.58771 EndZ=0
    g1: LineSegment StartX=-2.75 StartY=1.58771 StartZ=0 EndX=-2.75 EndY=-1.58771 EndZ=0
    g2: LineSegment StartX=-2.75 StartY=-1.58771 StartZ=0 EndX=0 EndY=-3.17543 EndZ=0
    g3: LineSegment StartX=0 StartY=-3.17543 StartZ=0 EndX=2.75 EndY=-1.58771 EndZ=0
    g4: LineSegment StartX=2.75 StartY=-1.58771 StartZ=0 EndX=2.75 EndY=1.58771 EndZ=0
    g5: LineSegment StartX=2.75 StartY=1.58771 StartZ=0 EndX=0 EndY=3.17543 EndZ=0
    g6: Circle [constr] CenterX=0 CenterY=0 CenterZ=0 NormalX=0 NormalY=0 NormalZ=1 AngleXU=0 Radius=3.17543
    g7: Circle CenterX=0 CenterY=0 CenterZ=0 NormalX=0 NormalY=0 NormalZ=1 AngleXU=0 Radius=1.5
  constraints (18):
    c: Coincident(g0,g1)
    c: Coincident(g1,g2)
    c: Coincident(g2,g3)
    c: Coincident(g3,g4)
    c: Coincident(g4,g5)
    c: Coincident(g5,g0)
    c: Equal(g0, g1-g5) x5
    c: PointOnObject(g0,g6)
    c: PointOnObject(g1,g6)
    c: PointOnObject(g2,g6)
    c: PointOnObject(g3,g6)
    c: PointOnObject(g4,g6)
    c: PointOnObject(g5,g6)
    c: Coincident(g6,g-1)
    c: PointOnObject(g5,g-2)
    c: DistanceX(g0,g4) = 5.5
    c: Coincident(g7,g-1)
    c: Radius(g7) = 1.5
FEATURE [PartDesign::Pad] Pad1142  label="M3 Nut Primitive233"
  Length = 1.2
  Length2 = 1.2
  Profile = -> Sketch2554
  Type = 4
FEATURE [Sketcher::SketchObject] Sketch2555
  ExternalGeometry = -> [Pad1142]
  MapMode = 5
  Placement = pos=(0,0,0) rot=(0.57735,0.57735,0.57735;2.0944rad)
  Support = -> [YZ_Plane1080]
  sketch-geometry (6):
    g0: LineSegment StartX=-2.67543 StartY=1.2 StartZ=0 EndX=-3.67543 EndY=1.2 EndZ=0
    g1: LineSegment StartX=-3.67543 StartY=1.2 StartZ=0 EndX=-3.67543 EndY=-1.2 EndZ=0
    g2: LineSegment StartX=-3.67543 StartY=-1.2 StartZ=0 EndX=-2.67543 EndY=-1.2 EndZ=0
    g3: LineSegment StartX=-2.67543 StartY=-1.2 StartZ=0 EndX=-3.17543 EndY=-1 EndZ=0
    g4: LineSegment StartX=-3.17543 StartY=-1 StartZ=0 EndX=-3.17543 EndY=1 EndZ=0
    g5: LineSegment StartX=-3.17543 StartY=1 StartZ=0 EndX=-2.67543 EndY=1.2 EndZ=0
  constraints (15):
    c: Horizontal(g0)
    c: Coincident(g0,g1)
    c: Coincident(g1,g2)
    c: Coincident(g2,g3)
    c: Coincident(g3,g4)
    c: Coincident(g4,g5)
    c: Coincident(g5,g0)
    c: Symmetric(g4,g3,g-1)
    c: Symmetric(g0,g2,g-1)
    c: Symmetric(g1,g0,g-1)
    c: DistanceX(g0,g4) = 0.5
    c: DistanceY(g3,g4) = 2
    c: DistanceY(g1,g0) = 2.4
    c: PointOnObject(g3,g-3)
    c: DistanceX(g4,g0) = 0.5
FEATURE [PartDesign::Groove] Groove241  label="M3 Nut Smooth233"
  Angle = 360
  Axis = (-2e-16,3e-16,1)
  Base = (0,0,0)
  BaseFeature = -> Pad1142
  Profile = -> Sketch2555
  ReferenceAxis = -> Sketch2555 [V_Axis]
  Reversed = true
FEATURE [PartDesign::Chamfer] Chamfer575  label="M3 Nut Smooth Hole233"
  Base = -> Groove241 [Edge24,Edge23]
  BaseFeature = -> Groove241
  Size = 0.2
FEATURE [PartDesign::Body] Body763  label="M3 Nut137"
  Group = -> [Sketch2554,Pad1142,Sketch2555,Groove241,Chamfer575]
  Origin = -> Origin1088
  Placement = pos=(-10,0,61.25) rot=(0,0,1;0rad)
  Tip = -> Chamfer575
FEATURE [Sketcher::SketchObject] Sketch2556
  MapMode = 5
  Support = -> [XY_Plane1087]
  sketch-geometry (8):
    g0: LineSegment StartX=0 StartY=3.17543 StartZ=0 EndX=-2.75 EndY=1.58771 EndZ=0
    g1: LineSegment StartX=-2.75 StartY=1.58771 StartZ=0 EndX=-2.75 EndY=-1.58771 EndZ=0
    g2: LineSegment StartX=-2.75 StartY=-1.58771 StartZ=0 EndX=0 EndY=-3.17543 EndZ=0
    g3: LineSegment StartX=0 StartY=-3.17543 StartZ=0 EndX=2.75 EndY=-1.58771 EndZ=0
    g4: LineSegment StartX=2.75 StartY=-1.58771 StartZ=0 EndX=2.75 EndY=1.58771 EndZ=0
    g5: LineSegment StartX=2.75 StartY=1.58771 StartZ=0 EndX=0 EndY=3.17543 EndZ=0
    g6: Circle [constr] CenterX=0 CenterY=0 CenterZ=0 NormalX=0 NormalY=0 NormalZ=1 AngleXU=0 Radius=3.17543
    g7: Circle CenterX=0 CenterY=0 CenterZ=0 NormalX=0 NormalY=0 NormalZ=1 AngleXU=0 Radius=1.5
  constraints (18):
    c: Coincident(g0,g1)
    c: Coincident(g1,g2)
    c: Coincident(g2,g3)
    c: Coincident(g3,g4)
    c: Coincident(g4,g5)
    c: Coincident(g5,g0)
    c: Equal(g0, g1-g5) x5
    c: PointOnObject(g0,g6)
    c: PointOnObject(g1,g6)
    c: PointOnObject(g2,g6)
    c: PointOnObject(g3,g6)
    c: PointOnObject(g4,g6)
    c: PointOnObject(g5,g6)
    c: Coincident(g6,g-1)
    c: PointOnObject(g5,g-2)
    c: DistanceX(g0,g4) = 5.5
    c: Coincident(g7,g-1)
    c: Radius(g7) = 1.5
FEATURE [PartDesign::Pad] Pad1143  label="M3 Nut Primitive234"
  Length = 1.2
  Length2 = 1.2
  Profile = -> Sketch2556
  Type = 4
FEATURE [Sketcher::SketchObject] Sketch2557
  ExternalGeometry = -> [Pad1143]
  MapMode = 5
  Placement = pos=(0,0,0) rot=(0.57735,0.57735,0.57735;2.0944rad)
  Support = -> [YZ_Plane1081]
  sketch-geometry (6):
    g0: LineSegment StartX=-2.67543 StartY=1.2 StartZ=0 EndX=-3.67543 EndY=1.2 EndZ=0
    g1: LineSegment StartX=-3.67543 StartY=1.2 StartZ=0 EndX=-3.67543 EndY=-1.2 EndZ=0
    g2: LineSegment StartX=-3.67543 StartY=-1.2 StartZ=0 EndX=-2.67543 EndY=-1.2 EndZ=0
    g3: LineSegment StartX=-2.67543 StartY=-1.2 StartZ=0 EndX=-3.17543 EndY=-1 EndZ=0
    g4: LineSegment StartX=-3.17543 StartY=-1 StartZ=0 EndX=-3.17543 EndY=1 EndZ=0
    g5: LineSegment StartX=-3.17543 StartY=1 StartZ=0 EndX=-2.67543 EndY=1.2 EndZ=0
  constraints (15):
    c: Horizontal(g0)
    c: Coincident(g0,g1)
    c: Coincident(g1,g2)
    c: Coincident(g2,g3)
    c: Coincident(g3,g4)
    c: Coincident(g4,g5)
    c: Coincident(g5,g0)
    c: Symmetric(g4,g3,g-1)
    c: Symmetric(g0,g2,g-1)
    c: Symmetric(g1,g0,g-1)
    c: DistanceX(g0,g4) = 0.5
    c: DistanceY(g3,g4) = 2
    c: DistanceY(g1,g0) = 2.4
    c: PointOnObject(g3,g-3)
    c: DistanceX(g4,g0) = 0.5
FEATURE [PartDesign::Groove] Groove242  label="M3 Nut Smooth234"
  Angle = 360
  Axis = (-2e-16,3e-16,1)
  Base = (0,0,0)
  BaseFeature = -> Pad1143
  Profile = -> Sketch2557
  ReferenceAxis = -> Sketch2557 [V_Axis]
  Reversed = true
FEATURE [PartDesign::Chamfer] Chamfer576  label="M3 Nut Smooth Hole234"
  Base = -> Groove242 [Edge24,Edge23]
  BaseFeature = -> Groove242
  Size = 0.2
FEATURE [PartDesign::Body] Body764  label="M3 Nut138"
  Group = -> [Sketch2556,Pad1143,Sketch2557,Groove242,Chamfer576]
  Origin = -> Origin1089
  Placement = pos=(-10,10,61) rot=(0,0,1;0rad)
  Tip = -> Chamfer576
FEATURE [Sketcher::SketchObject] Sketch2558
  MapMode = 5
  Support = -> [XY_Plane1088]
  sketch-geometry (8):
    g0: LineSegment StartX=0 StartY=3.17543 StartZ=0 EndX=-2.75 EndY=1.58771 EndZ=0
    g1: LineSegment StartX=-2.75 StartY=1.58771 StartZ=0 EndX=-2.75 EndY=-1.58771 EndZ=0
    g2: LineSegment StartX=-2.75 StartY=-1.58771 StartZ=0 EndX=0 EndY=-3.17543 EndZ=0
    g3: LineSegment StartX=0 StartY=-3.17543 StartZ=0 EndX=2.75 EndY=-1.58771 EndZ=0
    g4: LineSegment StartX=2.75 StartY=-1.58771 StartZ=0 EndX=2.75 EndY=1.58771 EndZ=0
    g5: LineSegment StartX=2.75 StartY=1.58771 StartZ=0 EndX=0 EndY=3.17543 EndZ=0
    g6: Circle [constr] CenterX=0 CenterY=0 CenterZ=0 NormalX=0 NormalY=0 NormalZ=1 AngleXU=0 Radius=3.17543
    g7: Circle CenterX=0 CenterY=0 CenterZ=0 NormalX=0 NormalY=0 NormalZ=1 AngleXU=0 Radius=1.5
  constraints (18):
    c: Coincident(g0,g1)
    c: Coincident(g1,g2)
    c: Coincident(g2,g3)
    c: Coincident(g3,g4)
    c: Coincident(g4,g5)
    c: Coincident(g5,g0)
    c: Equal(g0, g1-g5) x5
    c: PointOnObject(g0,g6)
    c: PointOnObject(g1,g6)
    c: PointOnObject(g2,g6)
    c: PointOnObject(g3,g6)
    c: PointOnObject(g4,g6)
    c: PointOnObject(g5,g6)
    c: Coincident(g6,g-1)
    c: PointOnObject(g5,g-2)
    c: DistanceX(g0,g4) = 5.5
    c: Coincident(g7,g-1)
    c: Radius(g7) = 1.5
FEATURE [PartDesign::Pad] Pad1144  label="M3 Nut Primitive235"
  Length = 1.2
  Length2 = 1.2
  Profile = -> Sketch2558
  Type = 4
FEATURE [Sketcher::SketchObject] Sketch2559
  ExternalGeometry = -> [Pad1144]
  MapMode = 5
  Placement = pos=(0,0,0) rot=(0.57735,0.57735,0.57735;2.0944rad)
  Support = -> [YZ_Plane1082]
  sketch-geometry (6):
    g0: LineSegment StartX=-2.67543 StartY=1.2 StartZ=0 EndX=-3.67543 EndY=1.2 EndZ=0
    g1: LineSegment StartX=-3.67543 StartY=1.2 StartZ=0 EndX=-3.67543 EndY=-1.2 EndZ=0
    g2: LineSegment StartX=-3.67543 StartY=-1.2 StartZ=0 EndX=-2.67543 EndY=-1.2 EndZ=0
    g3: LineSegment StartX=-2.67543 StartY=-1.2 StartZ=0 EndX=-3.17543 EndY=-1 EndZ=0
    g4: LineSegment StartX=-3.17543 StartY=-1 StartZ=0 EndX=-3.17543 EndY=1 EndZ=0
    g5: LineSegment StartX=-3.17543 StartY=1 StartZ=0 EndX=-2.67543 EndY=1.2 EndZ=0
  constraints (15):
    c: Horizontal(g0)
    c: Coincident(g0,g1)
    c: Coincident(g1,g2)
    c: Coincident(g2,g3)
    c: Coincident(g3,g4)
    c: Coincident(g4,g5)
    c: Coincident(g5,g0)
    c: Symmetric(g4,g3,g-1)
    c: Symmetric(g0,g2,g-1)
    c: Symmetric(g1,g0,g-1)
    c: DistanceX(g0,g4) = 0.5
    c: DistanceY(g3,g4) = 2
    c: DistanceY(g1,g0) = 2.4
    c: PointOnObject(g3,g-3)
    c: DistanceX(g4,g0) = 0.5
FEATURE [PartDesign::Groove] Groove243  label="M3 Nut Smooth235"
  Angle = 360
  Axis = (-2e-16,3e-16,1)
  Base = (0,0,0)
  BaseFeature = -> Pad1144
  Profile = -> Sketch2559
  ReferenceAxis = -> Sketch2559 [V_Axis]
  Reversed = true
FEATURE [PartDesign::Chamfer] Chamfer577  label="M3 Nut Smooth Hole235"
  Base = -> Groove243 [Edge24,Edge23]
  BaseFeature = -> Groove243
  Size = 0.2
FEATURE [PartDesign::Body] Body765  label="M3 Nut139"
  Group = -> [Sketch2558,Pad1144,Sketch2559,Groove243,Chamfer577]
  Origin = -> Origin1090
  Placement = pos=(20,0,61.25) rot=(0,0,1;0rad)
  Tip = -> Chamfer577
FEATURE [Sketcher::SketchObject] Sketch2560
  MapMode = 5
  Support = -> [XY_Plane1089]
  sketch-geometry (8):
    g0: LineSegment StartX=0 StartY=3.17543 StartZ=0 EndX=-2.75 EndY=1.58771 EndZ=0
    g1: LineSegment StartX=-2.75 StartY=1.58771 StartZ=0 EndX=-2.75 EndY=-1.58771 EndZ=0
    g2: LineSegment StartX=-2.75 StartY=-1.58771 StartZ=0 EndX=0 EndY=-3.17543 EndZ=0
    g3: LineSegment StartX=0 StartY=-3.17543 StartZ=0 EndX=2.75 EndY=-1.58771 EndZ=0
    g4: LineSegment StartX=2.75 StartY=-1.58771 StartZ=0 EndX=2.75 EndY=1.58771 EndZ=0
    g5: LineSegment StartX=2.75 StartY=1.58771 StartZ=0 EndX=0 EndY=3.17543 EndZ=0
    g6: Circle [constr] CenterX=0 CenterY=0 CenterZ=0 NormalX=0 NormalY=0 NormalZ=1 AngleXU=0 Radius=3.17543
    g7: Circle CenterX=0 CenterY=0 CenterZ=0 NormalX=0 NormalY=0 NormalZ=1 AngleXU=0 Radius=1.5
  constraints (18):
    c: Coincident(g0,g1)
    c: Coincident(g1,g2)
    c: Coincident(g2,g3)
    c: Coincident(g3,g4)
    c: Coincident(g4,g5)
    c: Coincident(g5,g0)
    c: Equal(g0, g1-g5) x5
    c: PointOnObject(g0,g6)
    c: PointOnObject(g1,g6)
    c: PointOnObject(g2,g6)
    c: PointOnObject(g3,g6)
    c: PointOnObject(g4,g6)
    c: PointOnObject(g5,g6)
    c: Coincident(g6,g-1)
    c: PointOnObject(g5,g-2)
    c: DistanceX(g0,g4) = 5.5
    c: Coincident(g7,g-1)
    c: Radius(g7) = 1.5
FEATURE [PartDesign::Pad] Pad1145  label="M3 Nut Primitive236"
  Length = 1.2
  Length2 = 1.2
  Profile = -> Sketch2560
  Type = 4
FEATURE [Sketcher::SketchObject] Sketch2561
  ExternalGeometry = -> [Pad1145]
  MapMode = 5
  Placement = pos=(0,0,0) rot=(0.57735,0.57735,0.57735;2.0944rad)
  Support = -> [YZ_Plane1083]
  sketch-geometry (6):
    g0: LineSegment StartX=-2.67543 StartY=1.2 StartZ=0 EndX=-3.67543 EndY=1.2 EndZ=0
    g1: LineSegment StartX=-3.67543 StartY=1.2 StartZ=0 EndX=-3.67543 EndY=-1.2 EndZ=0
    g2: LineSegment StartX=-3.67543 StartY=-1.2 StartZ=0 EndX=-2.67543 EndY=-1.2 EndZ=0
    g3: LineSegment StartX=-2.67543 StartY=-1.2 StartZ=0 EndX=-3.17543 EndY=-1 EndZ=0
    g4: LineSegment StartX=-3.17543 StartY=-1 StartZ=0 EndX=-3.17543 EndY=1 EndZ=0
    g5: LineSegment StartX=-3.17543 StartY=1 StartZ=0 EndX=-2.67543 EndY=1.2 EndZ=0
  constraints (15):
    c: Horizontal(g0)
    c: Coincident(g0,g1)
    c: Coincident(g1,g2)
    c: Coincident(g2,g3)
    c: Coincident(g3,g4)
    c: Coincident(g4,g5)
    c: Coincident(g5,g0)
    c: Symmetric(g4,g3,g-1)
    c: Symmetric(g0,g2,g-1)
    c: Symmetric(g1,g0,g-1)
    c: DistanceX(g0,g4) = 0.5
    c: DistanceY(g3,g4) = 2
    c: DistanceY(g1,g0) = 2.4
    c: PointOnObject(g3,g-3)
    c: DistanceX(g4,g0) = 0.5
FEATURE [PartDesign::Groove] Groove244  label="M3 Nut Smooth236"
  Angle = 360
  Axis = (-2e-16,3e-16,1)
  Base = (0,0,0)
  BaseFeature = -> Pad1145
  Profile = -> Sketch2561
  ReferenceAxis = -> Sketch2561 [V_Axis]
  Reversed = true
FEATURE [PartDesign::Chamfer] Chamfer578  label="M3 Nut Smooth Hole236"
  Base = -> Groove244 [Edge24,Edge23]
  BaseFeature = -> Groove244
  Size = 0.2
FEATURE [PartDesign::Body] Body766  label="M3 Nut140"
  Group = -> [Sketch2560,Pad1145,Sketch2561,Groove244,Chamfer578]
  Origin = -> Origin1091
  Placement = pos=(20,10,61.25) rot=(0,0,1;0rad)
  Tip = -> Chamfer578
FEATURE [App::Part] Part304  label="Front Cover Nuts"
  Group = -> [Body759,Body760,Body761,Body762,Body763,Body764,Body765,Body766]
  Origin = -> Origin1092
  Placement = pos=(-9,-95,171) rot=(0,0,1;4.71239rad)
FEATURE [Sketcher::SketchObject] Sketch2562
  MapMode = 5
  Support = -> [XY_Plane1093]
  sketch-geometry (8):
    g0: LineSegment StartX=0 StartY=3.17543 StartZ=0 EndX=-2.75 EndY=1.58771 EndZ=0
    g1: LineSegment StartX=-2.75 StartY=1.58771 StartZ=0 EndX=-2.75 EndY=-1.58771 EndZ=0
    g2: LineSegment StartX=-2.75 StartY=-1.58771 StartZ=0 EndX=0 EndY=-3.17543 EndZ=0
    g3: LineSegment StartX=0 StartY=-3.17543 StartZ=0 EndX=2.75 EndY=-1.58771 EndZ=0
    g4: LineSegment StartX=2.75 StartY=-1.58771 StartZ=0 EndX=2.75 EndY=1.58771 EndZ=0
    g5: LineSegment StartX=2.75 StartY=1.58771 StartZ=0 EndX=0 EndY=3.17543 EndZ=0
    g6: Circle [constr] CenterX=0 CenterY=0 CenterZ=0 NormalX=0 NormalY=0 NormalZ=1 AngleXU=0 Radius=3.17543
    g7: Circle CenterX=0 CenterY=0 CenterZ=0 NormalX=0 NormalY=0 NormalZ=1 AngleXU=0 Radius=1.5
  constraints (18):
    c: Coincident(g0,g1)
    c: Coincident(g1,g2)
    c: Coincident(g2,g3)
    c: Coincident(g3,g4)
    c: Coincident(g4,g5)
    c: Coincident(g5,g0)
    c: Equal(g0, g1-g5) x5
    c: PointOnObject(g0,g6)
    c: PointOnObject(g1,g6)
    c: PointOnObject(g2,g6)
    c: PointOnObject(g3,g6)
    c: PointOnObject(g4,g6)
    c: PointOnObject(g5,g6)
    c: Coincident(g6,g-1)
    c: PointOnObject(g5,g-2)
    c: DistanceX(g0,g4) = 5.5
    c: Coincident(g7,g-1)
    c: Radius(g7) = 1.5
FEATURE [Sketcher::SketchObject] Sketch2563
  MapMode = 5
  Support = -> [XY_Plane1098]
  sketch-geometry (8):
    g0: LineSegment StartX=0 StartY=3.17543 StartZ=0 EndX=-2.75 EndY=1.58771 EndZ=0
    g1: LineSegment StartX=-2.75 StartY=1.58771 StartZ=0 EndX=-2.75 EndY=-1.58771 EndZ=0
    g2: LineSegment StartX=-2.75 StartY=-1.58771 StartZ=0 EndX=0 EndY=-3.17543 EndZ=0
    g3: LineSegment StartX=0 StartY=-3.17543 StartZ=0 EndX=2.75 EndY=-1.58771 EndZ=0
    g4: LineSegment StartX=2.75 StartY=-1.58771 StartZ=0 EndX=2.75 EndY=1.58771 EndZ=0
    g5: LineSegment StartX=2.75 StartY=1.58771 StartZ=0 EndX=0 EndY=3.17543 EndZ=0
    g6: Circle [constr] CenterX=0 CenterY=0 CenterZ=0 NormalX=0 NormalY=0 NormalZ=1 AngleXU=0 Radius=3.17543
    g7: Circle CenterX=0 CenterY=0 CenterZ=0 NormalX=0 NormalY=0 NormalZ=1 AngleXU=0 Radius=1.5
  constraints (18):
    c: Coincident(g0,g1)
    c: Coincident(g1,g2)
    c: Coincident(g2,g3)
    c: Coincident(g3,g4)
    c: Coincident(g4,g5)
    c: Coincident(g5,g0)
    c: Equal(g0, g1-g5) x5
    c: PointOnObject(g0,g6)
    c: PointOnObject(g1,g6)
    c: PointOnObject(g2,g6)
    c: PointOnObject(g3,g6)
    c: PointOnObject(g4,g6)
    c: PointOnObject(g5,g6)
    c: Coincident(g6,g-1)
    c: PointOnObject(g5,g-2)
    c: DistanceX(g0,g4) = 5.5
    c: Coincident(g7,g-1)
    c: Radius(g7) = 1.5
FEATURE [Sketcher::SketchObject] Sketch2564
  MapMode = 5
  Support = -> [XY_Plane1099]
  sketch-geometry (8):
    g0: LineSegment StartX=0 StartY=3.17543 StartZ=0 EndX=-2.75 EndY=1.58771 EndZ=0
    g1: LineSegment StartX=-2.75 StartY=1.58771 StartZ=0 EndX=-2.75 EndY=-1.58771 EndZ=0
    g2: LineSegment StartX=-2.75 StartY=-1.58771 StartZ=0 EndX=0 EndY=-3.17543 EndZ=0
    g3: LineSegment StartX=0 StartY=-3.17543 StartZ=0 EndX=2.75 EndY=-1.58771 EndZ=0
    g4: LineSegment StartX=2.75 StartY=-1.58771 StartZ=0 EndX=2.75 EndY=1.58771 EndZ=0
    g5: LineSegment StartX=2.75 StartY=1.58771 StartZ=0 EndX=0 EndY=3.17543 EndZ=0
    g6: Circle [constr] CenterX=0 CenterY=0 CenterZ=0 NormalX=0 NormalY=0 NormalZ=1 AngleXU=0 Radius=3.17543
    g7: Circle CenterX=0 CenterY=0 CenterZ=0 NormalX=0 NormalY=0 NormalZ=1 AngleXU=0 Radius=1.5
  constraints (18):
    c: Coincident(g0,g1)
    c: Coincident(g1,g2)
    c: Coincident(g2,g3)
    c: Coincident(g3,g4)
    c: Coincident(g4,g5)
    c: Coincident(g5,g0)
    c: Equal(g0, g1-g5) x5
    c: PointOnObject(g0,g6)
    c: PointOnObject(g1,g6)
    c: PointOnObject(g2,g6)
    c: PointOnObject(g3,g6)
    c: PointOnObject(g4,g6)
    c: PointOnObject(g5,g6)
    c: Coincident(g6,g-1)
    c: PointOnObject(g5,g-2)
    c: DistanceX(g0,g4) = 5.5
    c: Coincident(g7,g-1)
    c: Radius(g7) = 1.5
FEATURE [Sketcher::SketchObject] Sketch2565
  MapMode = 5
  Support = -> [XY_Plane1091]
  sketch-geometry (8):
    g0: LineSegment StartX=0 StartY=3.17543 StartZ=0 EndX=-2.75 EndY=1.58771 EndZ=0
    g1: LineSegment StartX=-2.75 StartY=1.58771 StartZ=0 EndX=-2.75 EndY=-1.58771 EndZ=0
    g2: LineSegment StartX=-2.75 StartY=-1.58771 StartZ=0 EndX=0 EndY=-3.17543 EndZ=0
    g3: LineSegment StartX=0 StartY=-3.17543 StartZ=0 EndX=2.75 EndY=-1.58771 EndZ=0
    g4: LineSegment StartX=2.75 StartY=-1.58771 StartZ=0 EndX=2.75 EndY=1.58771 EndZ=0
    g5: LineSegment StartX=2.75 StartY=1.58771 StartZ=0 EndX=0 EndY=3.17543 EndZ=0
    g6: Circle [constr] CenterX=0 CenterY=0 CenterZ=0 NormalX=0 NormalY=0 NormalZ=1 AngleXU=0 Radius=3.17543
    g7: Circle CenterX=0 CenterY=0 CenterZ=0 NormalX=0 NormalY=0 NormalZ=1 AngleXU=0 Radius=1.5
  constraints (18):
    c: Coincident(g0,g1)
    c: Coincident(g1,g2)
    c: Coincident(g2,g3)
    c: Coincident(g3,g4)
    c: Coincident(g4,g5)
    c: Coincident(g5,g0)
    c: Equal(g0, g1-g5) x5
    c: PointOnObject(g0,g6)
    c: PointOnObject(g1,g6)
    c: PointOnObject(g2,g6)
    c: PointOnObject(g3,g6)
    c: PointOnObject(g4,g6)
    c: PointOnObject(g5,g6)
    c: Coincident(g6,g-1)
    c: PointOnObject(g5,g-2)
    c: DistanceX(g0,g4) = 5.5
    c: Coincident(g7,g-1)
    c: Radius(g7) = 1.5
FEATURE [Sketcher::SketchObject] Sketch2566
  MapMode = 5
  Support = -> [XY_Plane1094]
  sketch-geometry (8):
    g0: LineSegment StartX=0 StartY=3.17543 StartZ=0 EndX=-2.75 EndY=1.58771 EndZ=0
    g1: LineSegment StartX=-2.75 StartY=1.58771 StartZ=0 EndX=-2.75 EndY=-1.58771 EndZ=0
    g2: LineSegment StartX=-2.75 StartY=-1.58771 StartZ=0 EndX=0 EndY=-3.17543 EndZ=0
    g3: LineSegment StartX=0 StartY=-3.17543 StartZ=0 EndX=2.75 EndY=-1.58771 EndZ=0
    g4: LineSegment StartX=2.75 StartY=-1.58771 StartZ=0 EndX=2.75 EndY=1.58771 EndZ=0
    g5: LineSegment StartX=2.75 StartY=1.58771 StartZ=0 EndX=0 EndY=3.17543 EndZ=0
    g6: Circle [constr] CenterX=0 CenterY=0 CenterZ=0 NormalX=0 NormalY=0 NormalZ=1 AngleXU=0 Radius=3.17543
    g7: Circle CenterX=0 CenterY=0 CenterZ=0 NormalX=0 NormalY=0 NormalZ=1 AngleXU=0 Radius=1.5
  constraints (18):
    c: Coincident(g0,g1)
    c: Coincident(g1,g2)
    c: Coincident(g2,g3)
    c: Coincident(g3,g4)
    c: Coincident(g4,g5)
    c: Coincident(g5,g0)
    c: Equal(g0, g1-g5) x5
    c: PointOnObject(g0,g6)
    c: PointOnObject(g1,g6)
    c: PointOnObject(g2,g6)
    c: PointOnObject(g3,g6)
    c: PointOnObject(g4,g6)
    c: PointOnObject(g5,g6)
    c: Coincident(g6,g-1)
    c: PointOnObject(g5,g-2)
    c: DistanceX(g0,g4) = 5.5
    c: Coincident(g7,g-1)
    c: Radius(g7) = 1.5
FEATURE [Sketcher::SketchObject] Sketch2570
  MapMode = 5
  Support = -> [XY_Plane1096]
  sketch-geometry (8):
    g0: LineSegment StartX=0 StartY=3.17543 StartZ=0 EndX=-2.75 EndY=1.58771 EndZ=0
    g1: LineSegment StartX=-2.75 StartY=1.58771 StartZ=0 EndX=-2.75 EndY=-1.58771 EndZ=0
    g2: LineSegment StartX=-2.75 StartY=-1.58771 StartZ=0 EndX=0 EndY=-3.17543 EndZ=0
    g3: LineSegment StartX=0 StartY=-3.17543 StartZ=0 EndX=2.75 EndY=-1.58771 EndZ=0
    g4: LineSegment StartX=2.75 StartY=-1.58771 StartZ=0 EndX=2.75 EndY=1.58771 EndZ=0
    g5: LineSegment StartX=2.75 StartY=1.58771 StartZ=0 EndX=0 EndY=3.17543 EndZ=0
    g6: Circle [constr] CenterX=0 CenterY=0 CenterZ=0 NormalX=0 NormalY=0 NormalZ=1 AngleXU=0 Radius=3.17543
    g7: Circle CenterX=0 CenterY=0 CenterZ=0 NormalX=0 NormalY=0 NormalZ=1 AngleXU=0 Radius=1.5
  constraints (18):
    c: Coincident(g0,g1)
    c: Coincident(g1,g2)
    c: Coincident(g2,g3)
    c: Coincident(g3,g4)
    c: Coincident(g4,g5)
    c: Coincident(g5,g0)
    c: Equal(g0, g1-g5) x5
    c: PointOnObject(g0,g6)
    c: PointOnObject(g1,g6)
    c: PointOnObject(g2,g6)
    c: PointOnObject(g3,g6)
    c: PointOnObject(g4,g6)
    c: PointOnObject(g5,g6)
    c: Coincident(g6,g-1)
    c: PointOnObject(g5,g-2)
    c: DistanceX(g0,g4) = 5.5
    c: Coincident(g7,g-1)
    c: Radius(g7) = 1.5
FEATURE [Sketcher::SketchObject] Sketch2574
  MapMode = 5
  Support = -> [XY_Plane1095]
  sketch-geometry (8):
    g0: LineSegment StartX=0 StartY=3.17543 StartZ=0 EndX=-2.75 EndY=1.58771 EndZ=0
    g1: LineSegment StartX=-2.75 StartY=1.58771 StartZ=0 EndX=-2.75 EndY=-1.58771 EndZ=0
    g2: LineSegment StartX=-2.75 StartY=-1.58771 StartZ=0 EndX=0 EndY=-3.17543 EndZ=0
    g3: LineSegment StartX=0 StartY=-3.17543 StartZ=0 EndX=2.75 EndY=-1.58771 EndZ=0
    g4: LineSegment StartX=2.75 StartY=-1.58771 StartZ=0 EndX=2.75 EndY=1.58771 EndZ=0
    g5: LineSegment StartX=2.75 StartY=1.58771 StartZ=0 EndX=0 EndY=3.17543 EndZ=0
    g6: Circle [constr] CenterX=0 CenterY=0 CenterZ=0 NormalX=0 NormalY=0 NormalZ=1 AngleXU=0 Radius=3.17543
    g7: Circle CenterX=0 CenterY=0 CenterZ=0 NormalX=0 NormalY=0 NormalZ=1 AngleXU=0 Radius=1.5
  constraints (18):
    c: Coincident(g0,g1)
    c: Coincident(g1,g2)
    c: Coincident(g2,g3)
    c: Coincident(g3,g4)
    c: Coincident(g4,g5)
    c: Coincident(g5,g0)
    c: Equal(g0, g1-g5) x5
    c: PointOnObject(g0,g6)
    c: PointOnObject(g1,g6)
    c: PointOnObject(g2,g6)
    c: PointOnObject(g3,g6)
    c: PointOnObject(g4,g6)
    c: PointOnObject(g5,g6)
    c: Coincident(g6,g-1)
    c: PointOnObject(g5,g-2)
    c: DistanceX(g0,g4) = 5.5
    c: Coincident(g7,g-1)
    c: Radius(g7) = 1.5
FEATURE [Sketcher::SketchObject] Sketch2577
  MapMode = 5
  Support = -> [XY_Plane1097]
  sketch-geometry (8):
    g0: LineSegment StartX=0 StartY=3.17543 StartZ=0 EndX=-2.75 EndY=1.58771 EndZ=0
    g1: LineSegment StartX=-2.75 StartY=1.58771 StartZ=0 EndX=-2.75 EndY=-1.58771 EndZ=0
    g2: LineSegment StartX=-2.75 StartY=-1.58771 StartZ=0 EndX=0 EndY=-3.17543 EndZ=0
    g3: LineSegment StartX=0 StartY=-3.17543 StartZ=0 EndX=2.75 EndY=-1.58771 EndZ=0
    g4: LineSegment StartX=2.75 StartY=-1.58771 StartZ=0 EndX=2.75 EndY=1.58771 EndZ=0
    g5: LineSegment StartX=2.75 StartY=1.58771 StartZ=0 EndX=0 EndY=3.17543 EndZ=0
    g6: Circle [constr] CenterX=0 CenterY=0 CenterZ=0 NormalX=0 NormalY=0 NormalZ=1 AngleXU=0 Radius=3.17543
    g7: Circle CenterX=0 CenterY=0 CenterZ=0 NormalX=0 NormalY=0 NormalZ=1 AngleXU=0 Radius=1.5
  constraints (18):
    c: Coincident(g0,g1)
    c: Coincident(g1,g2)
    c: Coincident(g2,g3)
    c: Coincident(g3,g4)
    c: Coincident(g4,g5)
    c: Coincident(g5,g0)
    c: Equal(g0, g1-g5) x5
    c: PointOnObject(g0,g6)
    c: PointOnObject(g1,g6)
    c: PointOnObject(g2,g6)
    c: PointOnObject(g3,g6)
    c: PointOnObject(g4,g6)
    c: PointOnObject(g5,g6)
    c: Coincident(g6,g-1)
    c: PointOnObject(g5,g-2)
    c: DistanceX(g0,g4) = 5.5
    c: Coincident(g7,g-1)
    c: Radius(g7) = 1.5
FEATURE [PartDesign::Pad] Pad1146  label="M3 Nut Primitive237"
  Length = 1.2
  Length2 = 1.2
  Profile = -> Sketch2562
  Type = 4
FEATURE [Sketcher::SketchObject] Sketch2568
  ExternalGeometry = -> [Pad1146]
  MapMode = 5
  Placement = pos=(0,0,0) rot=(0.57735,0.57735,0.57735;2.0944rad)
  Support = -> [YZ_Plane1087]
  sketch-geometry (6):
    g0: LineSegment StartX=-2.67543 StartY=1.2 StartZ=0 EndX=-3.67543 EndY=1.2 EndZ=0
    g1: LineSegment StartX=-3.67543 StartY=1.2 StartZ=0 EndX=-3.67543 EndY=-1.2 EndZ=0
    g2: LineSegment StartX=-3.67543 StartY=-1.2 StartZ=0 EndX=-2.67543 EndY=-1.2 EndZ=0
    g3: LineSegment StartX=-2.67543 StartY=-1.2 StartZ=0 EndX=-3.17543 EndY=-1 EndZ=0
    g4: LineSegment StartX=-3.17543 StartY=-1 StartZ=0 EndX=-3.17543 EndY=1 EndZ=0
    g5: LineSegment StartX=-3.17543 StartY=1 StartZ=0 EndX=-2.67543 EndY=1.2 EndZ=0
  constraints (15):
    c: Horizontal(g0)
    c: Coincident(g0,g1)
    c: Coincident(g1,g2)
    c: Coincident(g2,g3)
    c: Coincident(g3,g4)
    c: Coincident(g4,g5)
    c: Coincident(g5,g0)
    c: Symmetric(g4,g3,g-1)
    c: Symmetric(g0,g2,g-1)
    c: Symmetric(g1,g0,g-1)
    c: DistanceX(g0,g4) = 0.5
    c: DistanceY(g3,g4) = 2
    c: DistanceY(g1,g0) = 2.4
    c: PointOnObject(g3,g-3)
    c: DistanceX(g4,g0) = 0.5
FEATURE [PartDesign::Pad] Pad1147  label="M3 Nut Primitive238"
  Length = 1.2
  Length2 = 1.2
  Profile = -> Sketch2563
  Type = 4
FEATURE [Sketcher::SketchObject] Sketch2571
  ExternalGeometry = -> [Pad1147]
  MapMode = 5
  Placement = pos=(0,0,0) rot=(0.57735,0.57735,0.57735;2.0944rad)
  Support = -> [YZ_Plane1089]
  sketch-geometry (6):
    g0: LineSegment StartX=-2.67543 StartY=1.2 StartZ=0 EndX=-3.67543 EndY=1.2 EndZ=0
    g1: LineSegment StartX=-3.67543 StartY=1.2 StartZ=0 EndX=-3.67543 EndY=-1.2 EndZ=0
    g2: LineSegment StartX=-3.67543 StartY=-1.2 StartZ=0 EndX=-2.67543 EndY=-1.2 EndZ=0
    g3: LineSegment StartX=-2.67543 StartY=-1.2 StartZ=0 EndX=-3.17543 EndY=-1 EndZ=0
    g4: LineSegment StartX=-3.17543 StartY=-1 StartZ=0 EndX=-3.17543 EndY=1 EndZ=0
    g5: LineSegment StartX=-3.17543 StartY=1 StartZ=0 EndX=-2.67543 EndY=1.2 EndZ=0
  constraints (15):
    c: Horizontal(g0)
    c: Coincident(g0,g1)
    c: Coincident(g1,g2)
    c: Coincident(g2,g3)
    c: Coincident(g3,g4)
    c: Coincident(g4,g5)
    c: Coincident(g5,g0)
    c: Symmetric(g4,g3,g-1)
    c: Symmetric(g0,g2,g-1)
    c: Symmetric(g1,g0,g-1)
    c: DistanceX(g0,g4) = 0.5
    c: DistanceY(g3,g4) = 2
    c: DistanceY(g1,g0) = 2.4
    c: PointOnObject(g3,g-3)
    c: DistanceX(g4,g0) = 0.5
FEATURE [PartDesign::Pad] Pad1148  label="M3 Nut Primitive239"
  Length = 1.2
  Length2 = 1.2
  Profile = -> Sketch2565
  Type = 4
FEATURE [Sketcher::SketchObject] Sketch2567
  ExternalGeometry = -> [Pad1148]
  MapMode = 5
  Placement = pos=(0,0,0) rot=(0.57735,0.57735,0.57735;2.0944rad)
  Support = -> [YZ_Plane1085]
  sketch-geometry (6):
    g0: LineSegment StartX=-2.67543 StartY=1.2 StartZ=0 EndX=-3.67543 EndY=1.2 EndZ=0
    g1: LineSegment StartX=-3.67543 StartY=1.2 StartZ=0 EndX=-3.67543 EndY=-1.2 EndZ=0
    g2: LineSegment StartX=-3.67543 StartY=-1.2 StartZ=0 EndX=-2.67543 EndY=-1.2 EndZ=0
    g3: LineSegment StartX=-2.67543 StartY=-1.2 StartZ=0 EndX=-3.17543 EndY=-1 EndZ=0
    g4: LineSegment StartX=-3.17543 StartY=-1 StartZ=0 EndX=-3.17543 EndY=1 EndZ=0
    g5: LineSegment StartX=-3.17543 StartY=1 StartZ=0 EndX=-2.67543 EndY=1.2 EndZ=0
  constraints (15):
    c: Horizontal(g0)
    c: Coincident(g0,g1)
    c: Coincident(g1,g2)
    c: Coincident(g2,g3)
    c: Coincident(g3,g4)
    c: Coincident(g4,g5)
    c: Coincident(g5,g0)
    c: Symmetric(g4,g3,g-1)
    c: Symmetric(g0,g2,g-1)
    c: Symmetric(g1,g0,g-1)
    c: DistanceX(g0,g4) = 0.5
    c: DistanceY(g3,g4) = 2
    c: DistanceY(g1,g0) = 2.4
    c: PointOnObject(g3,g-3)
    c: DistanceX(g4,g0) = 0.5
FEATURE [PartDesign::Groove] Groove245  label="M3 Nut Smooth237"
  Angle = 360
  Axis = (-2e-16,3e-16,1)
  Base = (0,0,0)
  BaseFeature = -> Pad1148
  Profile = -> Sketch2567
  ReferenceAxis = -> Sketch2567 [V_Axis]
  Reversed = true
FEATURE [PartDesign::Chamfer] Chamfer580  label="M3 Nut Smooth Hole238"
  Base = -> Groove245 [Edge24,Edge23]
  BaseFeature = -> Groove245
  Size = 0.2
FEATURE [PartDesign::Body] Body767  label="M3 Nut141"
  Group = -> [Sketch2565,Pad1148,Sketch2567,Groove245,Chamfer580]
  Origin = -> Origin1096
  Tip = -> Chamfer580
FEATURE [PartDesign::Groove] Groove248  label="M3 Nut Smooth240"
  Angle = 360
  Axis = (-2e-16,3e-16,1)
  Base = (0,0,0)
  BaseFeature = -> Pad1146
  Profile = -> Sketch2568
  ReferenceAxis = -> Sketch2568 [V_Axis]
  Reversed = true
FEATURE [PartDesign::Chamfer] Chamfer585  label="M3 Nut Smooth Hole243"
  Base = -> Groove248 [Edge24,Edge23]
  BaseFeature = -> Groove248
  Size = 0.2
FEATURE [PartDesign::Body] Body773  label="M3 Nut147"
  Group = -> [Sketch2562,Pad1146,Sketch2568,Groove248,Chamfer585]
  Origin = -> Origin1095
  Placement = pos=(0,10,0) rot=(0,0,1;0rad)
  Tip = -> Chamfer585
FEATURE [PartDesign::Pad] Pad1149  label="M3 Nut Primitive240"
  Length = 1.2
  Length2 = 1.2
  Profile = -> Sketch2566
  Type = 4
FEATURE [Sketcher::SketchObject] Sketch2569
  ExternalGeometry = -> [Pad1149]
  MapMode = 5
  Placement = pos=(0,0,0) rot=(0.57735,0.57735,0.57735;2.0944rad)
  Support = -> [YZ_Plane1088]
  sketch-geometry (6):
    g0: LineSegment StartX=-2.67543 StartY=1.2 StartZ=0 EndX=-3.67543 EndY=1.2 EndZ=0
    g1: LineSegment StartX=-3.67543 StartY=1.2 StartZ=0 EndX=-3.67543 EndY=-1.2 EndZ=0
    g2: LineSegment StartX=-3.67543 StartY=-1.2 StartZ=0 EndX=-2.67543 EndY=-1.2 EndZ=0
    g3: LineSegment StartX=-2.67543 StartY=-1.2 StartZ=0 EndX=-3.17543 EndY=-1 EndZ=0
    g4: LineSegment StartX=-3.17543 StartY=-1 StartZ=0 EndX=-3.17543 EndY=1 EndZ=0
    g5: LineSegment StartX=-3.17543 StartY=1 StartZ=0 EndX=-2.67543 EndY=1.2 EndZ=0
  constraints (15):
    c: Horizontal(g0)
    c: Coincident(g0,g1)
    c: Coincident(g1,g2)
    c: Coincident(g2,g3)
    c: Coincident(g3,g4)
    c: Coincident(g4,g5)
    c: Coincident(g5,g0)
    c: Symmetric(g4,g3,g-1)
    c: Symmetric(g0,g2,g-1)
    c: Symmetric(g1,g0,g-1)
    c: DistanceX(g0,g4) = 0.5
    c: DistanceY(g3,g4) = 2
    c: DistanceY(g1,g0) = 2.4
    c: PointOnObject(g3,g-3)
    c: DistanceX(g4,g0) = 0.5
FEATURE [PartDesign::Groove] Groove246  label="M3 Nut Smooth238"
  Angle = 360
  Axis = (-2e-16,3e-16,1)
  Base = (0,0,0)
  BaseFeature = -> Pad1149
  Profile = -> Sketch2569
  ReferenceAxis = -> Sketch2569 [V_Axis]
  Reversed = true
FEATURE [PartDesign::Chamfer] Chamfer584  label="M3 Nut Smooth Hole242"
  Base = -> Groove246 [Edge24,Edge23]
  BaseFeature = -> Groove246
  Size = 0.2
FEATURE [PartDesign::Body] Body771  label="M3 Nut145"
  Group = -> [Sketch2566,Pad1149,Sketch2569,Groove246,Chamfer584]
  Origin = -> Origin1094
  Placement = pos=(10,0,0) rot=(0,0,1;0rad)
  Tip = -> Chamfer584
FEATURE [PartDesign::Groove] Groove249  label="M3 Nut Smooth241"
  Angle = 360
  Axis = (-2e-16,3e-16,1)
  Base = (0,0,0)
  BaseFeature = -> Pad1147
  Profile = -> Sketch2571
  ReferenceAxis = -> Sketch2571 [V_Axis]
  Reversed = true
FEATURE [PartDesign::Chamfer] Chamfer581  label="M3 Nut Smooth Hole239"
  Base = -> Groove249 [Edge24,Edge23]
  BaseFeature = -> Groove249
  Size = 0.2
FEATURE [PartDesign::Body] Body768  label="M3 Nut142"
  Group = -> [Sketch2563,Pad1147,Sketch2571,Groove249,Chamfer581]
  Origin = -> Origin1098
  Placement = pos=(10,10,0) rot=(0,0,1;0rad)
  Tip = -> Chamfer581
FEATURE [PartDesign::Pad] Pad1150  label="M3 Nut Primitive241"
  Length = 1.2
  Length2 = 1.2
  Profile = -> Sketch2570
  Type = 4
FEATURE [Sketcher::SketchObject] Sketch2572
  ExternalGeometry = -> [Pad1150]
  MapMode = 5
  Placement = pos=(0,0,0) rot=(0.57735,0.57735,0.57735;2.0944rad)
  Support = -> [YZ_Plane1091]
  sketch-geometry (6):
    g0: LineSegment StartX=-2.67543 StartY=1.2 StartZ=0 EndX=-3.67543 EndY=1.2 EndZ=0
    g1: LineSegment StartX=-3.67543 StartY=1.2 StartZ=0 EndX=-3.67543 EndY=-1.2 EndZ=0
    g2: LineSegment StartX=-3.67543 StartY=-1.2 StartZ=0 EndX=-2.67543 EndY=-1.2 EndZ=0
    g3: LineSegment StartX=-2.67543 StartY=-1.2 StartZ=0 EndX=-3.17543 EndY=-1 EndZ=0
    g4: LineSegment StartX=-3.17543 StartY=-1 StartZ=0 EndX=-3.17543 EndY=1 EndZ=0
    g5: LineSegment StartX=-3.17543 StartY=1 StartZ=0 EndX=-2.67543 EndY=1.2 EndZ=0
  constraints (15):
    c: Horizontal(g0)
    c: Coincident(g0,g1)
    c: Coincident(g1,g2)
    c: Coincident(g2,g3)
    c: Coincident(g3,g4)
    c: Coincident(g4,g5)
    c: Coincident(g5,g0)
    c: Symmetric(g4,g3,g-1)
    c: Symmetric(g0,g2,g-1)
    c: Symmetric(g1,g0,g-1)
    c: DistanceX(g0,g4) = 0.5
    c: DistanceY(g3,g4) = 2
    c: DistanceY(g1,g0) = 2.4
    c: PointOnObject(g3,g-3)
    c: DistanceX(g4,g0) = 0.5
FEATURE [PartDesign::Groove] Groove247  label="M3 Nut Smooth239"
  Angle = 360
  Axis = (-2e-16,3e-16,1)
  Base = (0,0,0)
  BaseFeature = -> Pad1150
  Profile = -> Sketch2572
  ReferenceAxis = -> Sketch2572 [V_Axis]
  Reversed = true
FEATURE [PartDesign::Chamfer] Chamfer582  label="M3 Nut Smooth Hole240"
  Base = -> Groove247 [Edge24,Edge23]
  BaseFeature = -> Groove247
  Size = 0.2
FEATURE [PartDesign::Body] Body774  label="M3 Nut148"
  Group = -> [Sketch2570,Pad1150,Sketch2572,Groove247,Chamfer582]
  Origin = -> Origin1099
  Placement = pos=(-10,0,61.25) rot=(0,0,1;0rad)
  Tip = -> Chamfer582
FEATURE [PartDesign::Pad] Pad1151  label="M3 Nut Primitive242"
  Length = 1.2
  Length2 = 1.2
  Profile = -> Sketch2574
  Type = 4
FEATURE [Sketcher::SketchObject] Sketch2575
  ExternalGeometry = -> [Pad1151]
  MapMode = 5
  Placement = pos=(0,0,0) rot=(0.57735,0.57735,0.57735;2.0944rad)
  Support = -> [YZ_Plane1090]
  sketch-geometry (6):
    g0: LineSegment StartX=-2.67543 StartY=1.2 StartZ=0 EndX=-3.67543 EndY=1.2 EndZ=0
    g1: LineSegment StartX=-3.67543 StartY=1.2 StartZ=0 EndX=-3.67543 EndY=-1.2 EndZ=0
    g2: LineSegment StartX=-3.67543 StartY=-1.2 StartZ=0 EndX=-2.67543 EndY=-1.2 EndZ=0
    g3: LineSegment StartX=-2.67543 StartY=-1.2 StartZ=0 EndX=-3.17543 EndY=-1 EndZ=0
    g4: LineSegment StartX=-3.17543 StartY=-1 StartZ=0 EndX=-3.17543 EndY=1 EndZ=0
    g5: LineSegment StartX=-3.17543 StartY=1 StartZ=0 EndX=-2.67543 EndY=1.2 EndZ=0
  constraints (15):
    c: Horizontal(g0)
    c: Coincident(g0,g1)
    c: Coincident(g1,g2)
    c: Coincident(g2,g3)
    c: Coincident(g3,g4)
    c: Coincident(g4,g5)
    c: Coincident(g5,g0)
    c: Symmetric(g4,g3,g-1)
    c: Symmetric(g0,g2,g-1)
    c: Symmetric(g1,g0,g-1)
    c: DistanceX(g0,g4) = 0.5
    c: DistanceY(g3,g4) = 2
    c: DistanceY(g1,g0) = 2.4
    c: PointOnObject(g3,g-3)
    c: DistanceX(g4,g0) = 0.5
FEATURE [PartDesign::Pad] Pad1152  label="M3 Nut Primitive243"
  Length = 1.2
  Length2 = 1.2
  Profile = -> Sketch2577
  Type = 4
FEATURE [Sketcher::SketchObject] Sketch2573
  ExternalGeometry = -> [Pad1152]
  MapMode = 5
  Placement = pos=(0,0,0) rot=(0.57735,0.57735,0.57735;2.0944rad)
  Support = -> [YZ_Plane1092]
  sketch-geometry (6):
    g0: LineSegment StartX=-2.67543 StartY=1.2 StartZ=0 EndX=-3.67543 EndY=1.2 EndZ=0
    g1: LineSegment StartX=-3.67543 StartY=1.2 StartZ=0 EndX=-3.67543 EndY=-1.2 EndZ=0
    g2: LineSegment StartX=-3.67543 StartY=-1.2 StartZ=0 EndX=-2.67543 EndY=-1.2 EndZ=0
    g3: LineSegment StartX=-2.67543 StartY=-1.2 StartZ=0 EndX=-3.17543 EndY=-1 EndZ=0
    g4: LineSegment StartX=-3.17543 StartY=-1 StartZ=0 EndX=-3.17543 EndY=1 EndZ=0
    g5: LineSegment StartX=-3.17543 StartY=1 StartZ=0 EndX=-2.67543 EndY=1.2 EndZ=0
  constraints (15):
    c: Horizontal(g0)
    c: Coincident(g0,g1)
    c: Coincident(g1,g2)
    c: Coincident(g2,g3)
    c: Coincident(g3,g4)
    c: Coincident(g4,g5)
    c: Coincident(g5,g0)
    c: Symmetric(g4,g3,g-1)
    c: Symmetric(g0,g2,g-1)
    c: Symmetric(g1,g0,g-1)
    c: DistanceX(g0,g4) = 0.5
    c: DistanceY(g3,g4) = 2
    c: DistanceY(g1,g0) = 2.4
    c: PointOnObject(g3,g-3)
    c: DistanceX(g4,g0) = 0.5
FEATURE [PartDesign::Groove] Groove250  label="M3 Nut Smooth242"
  Angle = 360
  Axis = (-2e-16,3e-16,1)
  Base = (0,0,0)
  BaseFeature = -> Pad1152
  Profile = -> Sketch2573
  ReferenceAxis = -> Sketch2573 [V_Axis]
  Reversed = true
FEATURE [PartDesign::Chamfer] Chamfer586  label="M3 Nut Smooth Hole244"
  Base = -> Groove250 [Edge24,Edge23]
  BaseFeature = -> Groove250
  Size = 0.2
FEATURE [PartDesign::Body] Body770  label="M3 Nut144"
  Group = -> [Sketch2577,Pad1152,Sketch2573,Groove250,Chamfer586]
  Origin = -> Origin1097
  Placement = pos=(20,0,61.25) rot=(0,0,1;0rad)
  Tip = -> Chamfer586
FEATURE [PartDesign::Pad] Pad1153  label="M3 Nut Primitive244"
  Length = 1.2
  Length2 = 1.2
  Profile = -> Sketch2564
  Type = 4
FEATURE [Sketcher::SketchObject] Sketch2576
  ExternalGeometry = -> [Pad1153]
  MapMode = 5
  Placement = pos=(0,0,0) rot=(0.57735,0.57735,0.57735;2.0944rad)
  Support = -> [YZ_Plane1093]
  sketch-geometry (6):
    g0: LineSegment StartX=-2.67543 StartY=1.2 StartZ=0 EndX=-3.67543 EndY=1.2 EndZ=0
    g1: LineSegment StartX=-3.67543 StartY=1.2 StartZ=0 EndX=-3.67543 EndY=-1.2 EndZ=0
    g2: LineSegment StartX=-3.67543 StartY=-1.2 StartZ=0 EndX=-2.67543 EndY=-1.2 EndZ=0
    g3: LineSegment StartX=-2.67543 StartY=-1.2 StartZ=0 EndX=-3.17543 EndY=-1 EndZ=0
    g4: LineSegment StartX=-3.17543 StartY=-1 StartZ=0 EndX=-3.17543 EndY=1 EndZ=0
    g5: LineSegment StartX=-3.17543 StartY=1 StartZ=0 EndX=-2.67543 EndY=1.2 EndZ=0
  constraints (15):
    c: Horizontal(g0)
    c: Coincident(g0,g1)
    c: Coincident(g1,g2)
    c: Coincident(g2,g3)
    c: Coincident(g3,g4)
    c: Coincident(g4,g5)
    c: Coincident(g5,g0)
    c: Symmetric(g4,g3,g-1)
    c: Symmetric(g0,g2,g-1)
    c: Symmetric(g1,g0,g-1)
    c: DistanceX(g0,g4) = 0.5
    c: DistanceY(g3,g4) = 2
    c: DistanceY(g1,g0) = 2.4
    c: PointOnObject(g3,g-3)
    c: DistanceX(g4,g0) = 0.5
FEATURE [PartDesign::Groove] Groove251  label="M3 Nut Smooth243"
  Angle = 360
  Axis = (-2e-16,3e-16,1)
  Base = (0,0,0)
  BaseFeature = -> Pad1151
  Profile = -> Sketch2575
  ReferenceAxis = -> Sketch2575 [V_Axis]
  Reversed = true
FEATURE [PartDesign::Chamfer] Chamfer583  label="M3 Nut Smooth Hole241"
  Base = -> Groove251 [Edge24,Edge23]
  BaseFeature = -> Groove251
  Size = 0.2
FEATURE [PartDesign::Body] Body772  label="M3 Nut146"
  Group = -> [Sketch2574,Pad1151,Sketch2575,Groove251,Chamfer583]
  Origin = -> Origin1093
  Placement = pos=(20,10,61.25) rot=(0,0,1;0rad)
  Tip = -> Chamfer583
FEATURE [PartDesign::Groove] Groove252  label="M3 Nut Smooth244"
  Angle = 360
  Axis = (-2e-16,3e-16,1)
  Base = (0,0,0)
  BaseFeature = -> Pad1153
  Profile = -> Sketch2576
  ReferenceAxis = -> Sketch2576 [V_Axis]
  Reversed = true
FEATURE [PartDesign::Chamfer] Chamfer579  label="M3 Nut Smooth Hole237"
  Base = -> Groove252 [Edge24,Edge23]
  BaseFeature = -> Groove252
  Size = 0.2
FEATURE [PartDesign::Body] Body769  label="M3 Nut143"
  Group = -> [Sketch2564,Pad1153,Sketch2576,Groove252,Chamfer579]
  Origin = -> Origin1100
  Placement = pos=(-10,10,61) rot=(0,0,1;0rad)
  Tip = -> Chamfer579
FEATURE [App::Part] Part305  label="Rear Cover Nuts001"
  Group = -> [Body767,Body773,Body771,Body768,Body774,Body769,Body770,Body772]
  Origin = -> Origin1101
  Placement = pos=(-216.75,-95,171) rot=(0,0,1;4.71239rad)
FEATURE [App::Part] Part303  label="Cover Nuts"
  Group = -> [Part304,Part305]
  Origin = -> Origin1083
FEATURE [Sketcher::SketchObject] Sketch2580
  MapMode = 5
  Support = -> [XY_Plane1100]
  sketch-geometry (1):
    g0: Circle CenterX=0 CenterY=0 CenterZ=0 NormalX=0 NormalY=0 NormalZ=1 AngleXU=0 Radius=2.75
  constraints (2):
    c: Coincident(g0,g-1)
    c: Radius(g0) = 2.75
FEATURE [PartDesign::Pad] Pad1154  label="M3x8 Head179"
  Length = 3
  Length2 = 100
  Profile = -> Sketch2580
  Type = 0
FEATURE [Sketcher::SketchObject] Sketch2579
  MapMode = 5
  Placement = pos=(0,0,3) rot=(0,0,1;0rad)
  Support = -> [Pad1154]
  sketch-geometry (1):
    g0: Circle CenterX=0 CenterY=0 CenterZ=0 NormalX=0 NormalY=0 NormalZ=1 AngleXU=0 Radius=1.5
  constraints (2):
    c: Coincident(g0,g-1)
    c: Radius(g0) = 1.5
FEATURE [PartDesign::Pad] Pad1155  label="M3x8 Thread179"
  BaseFeature = -> Pad1154
  Length = 8
  Length2 = 100
  Profile = -> Sketch2579
  Type = 0
FEATURE [Sketcher::SketchObject] Sketch2578
  MapMode = 5
  Placement = pos=(0,0,0) rot=(1,0,0;3.14159rad)
  Support = -> [Pad1155]
  sketch-geometry (7):
    g0: LineSegment StartX=1.275 StartY=0.736122 StartZ=0 EndX=0 EndY=1.47224 EndZ=0
    g1: LineSegment StartX=0 StartY=1.47224 StartZ=0 EndX=-1.275 EndY=0.736122 EndZ=0
    g2: LineSegment StartX=-1.275 StartY=0.736122 StartZ=0 EndX=-1.275 EndY=-0.736122 EndZ=0
    g3: LineSegment StartX=-1.275 StartY=-0.736122 StartZ=0 EndX=1.34766e-11 EndY=-1.47224 EndZ=0
    g4: LineSegment StartX=1.34766e-11 StartY=-1.47224 StartZ=0 EndX=1.275 EndY=-0.736122 EndZ=0
    g5: LineSegment StartX=1.275 StartY=-0.736122 StartZ=0 EndX=1.275 EndY=0.736122 EndZ=0
    g6: Circle [constr] CenterX=0 CenterY=0 CenterZ=0 NormalX=0 NormalY=0 NormalZ=1 AngleXU=0 Radius=1.47224
  constraints (16):
    c: Coincident(g0,g1)
    c: Coincident(g1,g2)
    c: Coincident(g2,g3)
    c: Coincident(g3,g4)
    c: Coincident(g4,g5)
    c: Coincident(g5,g0)
    c: Equal(g0, g1-g5) x5
    c: PointOnObject(g0,g6)
    c: PointOnObject(g1,g6)
    c: PointOnObject(g2,g6)
    c: PointOnObject(g3,g6)
    c: PointOnObject(g4,g6)
    c: PointOnObject(g5,g6)
    c: Coincident(g6,g-1)
    c: PointOnObject(g0,g-2)
    c: DistanceX(g1,g0) = 2.55
FEATURE [PartDesign::Pocket] Pocket905  label="M3x8 Wrench179"
  BaseFeature = -> Pad1155
  Length = 1.3
  Length2 = 100
  Profile = -> Sketch2578
  Type = 0
FEATURE [PartDesign::Chamfer] Chamfer587  label="M3x8 Smooth178"
  Base = -> Pocket905 [Face11,Edge2,Edge24,Edge3]
  BaseFeature = -> Pocket905
  Size = 0.2
FEATURE [PartDesign::Body] Body775  label="M3x151"
  Group = -> [Sketch2580,Pad1154,Sketch2579,Pad1155,Sketch2578,Pocket905,Chamfer587]
  Origin = -> Origin1102
  Placement = pos=(0,0,-4.25) rot=(0,0,1;0rad)
  Tip = -> Chamfer587
FEATURE [Sketcher::SketchObject] Sketch2583
  MapMode = 5
  Support = -> [XY_Plane1101]
  sketch-geometry (1):
    g0: Circle CenterX=0 CenterY=0 CenterZ=0 NormalX=0 NormalY=0 NormalZ=1 AngleXU=0 Radius=2.75
  constraints (2):
    c: Coincident(g0,g-1)
    c: Radius(g0) = 2.75
FEATURE [PartDesign::Pad] Pad1156  label="M3x8 Head180"
  Length = 3
  Length2 = 100
  Profile = -> Sketch2583
  Type = 0
FEATURE [Sketcher::SketchObject] Sketch2582
  MapMode = 5
  Placement = pos=(0,0,3) rot=(0,0,1;0rad)
  Support = -> [Pad1156]
  sketch-geometry (1):
    g0: Circle CenterX=0 CenterY=0 CenterZ=0 NormalX=0 NormalY=0 NormalZ=1 AngleXU=0 Radius=1.5
  constraints (2):
    c: Coincident(g0,g-1)
    c: Radius(g0) = 1.5
FEATURE [PartDesign::Pad] Pad1157  label="M3x8 Thread180"
  BaseFeature = -> Pad1156
  Length = 8
  Length2 = 100
  Profile = -> Sketch2582
  Type = 0
FEATURE [Sketcher::SketchObject] Sketch2581
  MapMode = 5
  Placement = pos=(0,0,0) rot=(1,0,0;3.14159rad)
  Support = -> [Pad1157]
  sketch-geometry (7):
    g0: LineSegment StartX=1.275 StartY=0.736122 StartZ=0 EndX=0 EndY=1.47224 EndZ=0
    g1: LineSegment StartX=0 StartY=1.47224 StartZ=0 EndX=-1.275 EndY=0.736122 EndZ=0
    g2: LineSegment StartX=-1.275 StartY=0.736122 StartZ=0 EndX=-1.275 EndY=-0.736122 EndZ=0
    g3: LineSegment StartX=-1.275 StartY=-0.736122 StartZ=0 EndX=1.34766e-11 EndY=-1.47224 EndZ=0
    g4: LineSegment StartX=1.34766e-11 StartY=-1.47224 StartZ=0 EndX=1.275 EndY=-0.736122 EndZ=0
    g5: LineSegment StartX=1.275 StartY=-0.736122 StartZ=0 EndX=1.275 EndY=0.736122 EndZ=0
    g6: Circle [constr] CenterX=0 CenterY=0 CenterZ=0 NormalX=0 NormalY=0 NormalZ=1 AngleXU=0 Radius=1.47224
  constraints (16):
    c: Coincident(g0,g1)
    c: Coincident(g1,g2)
    c: Coincident(g2,g3)
    c: Coincident(g3,g4)
    c: Coincident(g4,g5)
    c: Coincident(g5,g0)
    c: Equal(g0, g1-g5) x5
    c: PointOnObject(g0,g6)
    c: PointOnObject(g1,g6)
    c: PointOnObject(g2,g6)
    c: PointOnObject(g3,g6)
    c: PointOnObject(g4,g6)
    c: PointOnObject(g5,g6)
    c: Coincident(g6,g-1)
    c: PointOnObject(g0,g-2)
    c: DistanceX(g1,g0) = 2.55
FEATURE [PartDesign::Pocket] Pocket906  label="M3x8 Wrench180"
  BaseFeature = -> Pad1157
  Length = 1.3
  Length2 = 100
  Profile = -> Sketch2581
  Type = 0
FEATURE [PartDesign::Chamfer] Chamfer588  label="M3x8 Smooth179"
  Base = -> Pocket906 [Face11,Edge2,Edge24,Edge3]
  BaseFeature = -> Pocket906
  Size = 0.2
FEATURE [PartDesign::Body] Body776  label="M3x152"
  Group = -> [Sketch2583,Pad1156,Sketch2582,Pad1157,Sketch2581,Pocket906,Chamfer588]
  Origin = -> Origin1103
  Placement = pos=(0,10,-4.25) rot=(0,0,1;0rad)
  Tip = -> Chamfer588
FEATURE [Sketcher::SketchObject] Sketch2586
  MapMode = 5
  Support = -> [XY_Plane1102]
  sketch-geometry (1):
    g0: Circle CenterX=0 CenterY=0 CenterZ=0 NormalX=0 NormalY=0 NormalZ=1 AngleXU=0 Radius=2.75
  constraints (2):
    c: Coincident(g0,g-1)
    c: Radius(g0) = 2.75
FEATURE [PartDesign::Pad] Pad1158  label="M3x8 Head181"
  Length = 3
  Length2 = 100
  Profile = -> Sketch2586
  Type = 0
FEATURE [Sketcher::SketchObject] Sketch2585
  MapMode = 5
  Placement = pos=(0,0,3) rot=(0,0,1;0rad)
  Support = -> [Pad1158]
  sketch-geometry (1):
    g0: Circle CenterX=0 CenterY=0 CenterZ=0 NormalX=0 NormalY=0 NormalZ=1 AngleXU=0 Radius=1.5
  constraints (2):
    c: Coincident(g0,g-1)
    c: Radius(g0) = 1.5
FEATURE [PartDesign::Pad] Pad1159  label="M3x8 Thread181"
  BaseFeature = -> Pad1158
  Length = 8
  Length2 = 100
  Profile = -> Sketch2585
  Type = 0
FEATURE [Sketcher::SketchObject] Sketch2584
  MapMode = 5
  Placement = pos=(0,0,0) rot=(1,0,0;3.14159rad)
  Support = -> [Pad1159]
  sketch-geometry (7):
    g0: LineSegment StartX=1.275 StartY=0.736122 StartZ=0 EndX=0 EndY=1.47224 EndZ=0
    g1: LineSegment StartX=0 StartY=1.47224 StartZ=0 EndX=-1.275 EndY=0.736122 EndZ=0
    g2: LineSegment StartX=-1.275 StartY=0.736122 StartZ=0 EndX=-1.275 EndY=-0.736122 EndZ=0
    g3: LineSegment StartX=-1.275 StartY=-0.736122 StartZ=0 EndX=1.34766e-11 EndY=-1.47224 EndZ=0
    g4: LineSegment StartX=1.34766e-11 StartY=-1.47224 StartZ=0 EndX=1.275 EndY=-0.736122 EndZ=0
    g5: LineSegment StartX=1.275 StartY=-0.736122 StartZ=0 EndX=1.275 EndY=0.736122 EndZ=0
    g6: Circle [constr] CenterX=0 CenterY=0 CenterZ=0 NormalX=0 NormalY=0 NormalZ=1 AngleXU=0 Radius=1.47224
  constraints (16):
    c: Coincident(g0,g1)
    c: Coincident(g1,g2)
    c: Coincident(g2,g3)
    c: Coincident(g3,g4)
    c: Coincident(g4,g5)
    c: Coincident(g5,g0)
    c: Equal(g0, g1-g5) x5
    c: PointOnObject(g0,g6)
    c: PointOnObject(g1,g6)
    c: PointOnObject(g2,g6)
    c: PointOnObject(g3,g6)
    c: PointOnObject(g4,g6)
    c: PointOnObject(g5,g6)
    c: Coincident(g6,g-1)
    c: PointOnObject(g0,g-2)
    c: DistanceX(g1,g0) = 2.55
FEATURE [PartDesign::Pocket] Pocket907  label="M3x8 Wrench181"
  BaseFeature = -> Pad1159
  Length = 1.3
  Length2 = 100
  Profile = -> Sketch2584
  Type = 0
FEATURE [PartDesign::Chamfer] Chamfer589  label="M3x8 Smooth180"
  Base = -> Pocket907 [Face11,Edge2,Edge24,Edge3]
  BaseFeature = -> Pocket907
  Size = 0.2
FEATURE [PartDesign::Body] Body777  label="M3x153"
  Group = -> [Sketch2586,Pad1158,Sketch2585,Pad1159,Sketch2584,Pocket907,Chamfer589]
  Origin = -> Origin1104
  Placement = pos=(-9.3e-15,-10,76.2) rot=(0,1,0;3.14159rad)
  Tip = -> Chamfer589
FEATURE [Sketcher::SketchObject] Sketch2589
  MapMode = 5
  Support = -> [XY_Plane1103]
  sketch-geometry (1):
    g0: Circle CenterX=0 CenterY=0 CenterZ=0 NormalX=0 NormalY=0 NormalZ=1 AngleXU=0 Radius=2.75
  constraints (2):
    c: Coincident(g0,g-1)
    c: Radius(g0) = 2.75
FEATURE [PartDesign::Pad] Pad1160  label="M3x8 Head182"
  Length = 3
  Length2 = 100
  Profile = -> Sketch2589
  Type = 0
FEATURE [Sketcher::SketchObject] Sketch2588
  MapMode = 5
  Placement = pos=(0,0,3) rot=(0,0,1;0rad)
  Support = -> [Pad1160]
  sketch-geometry (1):
    g0: Circle CenterX=0 CenterY=0 CenterZ=0 NormalX=0 NormalY=0 NormalZ=1 AngleXU=0 Radius=1.5
  constraints (2):
    c: Coincident(g0,g-1)
    c: Radius(g0) = 1.5
FEATURE [PartDesign::Pad] Pad1161  label="M3x8 Thread182"
  BaseFeature = -> Pad1160
  Length = 8
  Length2 = 100
  Profile = -> Sketch2588
  Type = 0
FEATURE [Sketcher::SketchObject] Sketch2587
  MapMode = 5
  Placement = pos=(0,0,0) rot=(1,0,0;3.14159rad)
  Support = -> [Pad1161]
  sketch-geometry (7):
    g0: LineSegment StartX=1.275 StartY=0.736122 StartZ=0 EndX=0 EndY=1.47224 EndZ=0
    g1: LineSegment StartX=0 StartY=1.47224 StartZ=0 EndX=-1.275 EndY=0.736122 EndZ=0
    g2: LineSegment StartX=-1.275 StartY=0.736122 StartZ=0 EndX=-1.275 EndY=-0.736122 EndZ=0
    g3: LineSegment StartX=-1.275 StartY=-0.736122 StartZ=0 EndX=1.34766e-11 EndY=-1.47224 EndZ=0
    g4: LineSegment StartX=1.34766e-11 StartY=-1.47224 StartZ=0 EndX=1.275 EndY=-0.736122 EndZ=0
    g5: LineSegment StartX=1.275 StartY=-0.736122 StartZ=0 EndX=1.275 EndY=0.736122 EndZ=0
    g6: Circle [constr] CenterX=0 CenterY=0 CenterZ=0 NormalX=0 NormalY=0 NormalZ=1 AngleXU=0 Radius=1.47224
  constraints (16):
    c: Coincident(g0,g1)
    c: Coincident(g1,g2)
    c: Coincident(g2,g3)
    c: Coincident(g3,g4)
    c: Coincident(g4,g5)
    c: Coincident(g5,g0)
    c: Equal(g0, g1-g5) x5
    c: PointOnObject(g0,g6)
    c: PointOnObject(g1,g6)
    c: PointOnObject(g2,g6)
    c: PointOnObject(g3,g6)
    c: PointOnObject(g4,g6)
    c: PointOnObject(g5,g6)
    c: Coincident(g6,g-1)
    c: PointOnObject(g0,g-2)
    c: DistanceX(g1,g0) = 2.55
FEATURE [PartDesign::Pocket] Pocket908  label="M3x8 Wrench182"
  BaseFeature = -> Pad1161
  Length = 1.3
  Length2 = 100
  Profile = -> Sketch2587
  Type = 0
FEATURE [PartDesign::Chamfer] Chamfer590  label="M3x8 Smooth181"
  Base = -> Pocket908 [Face11,Edge2,Edge24,Edge3]
  BaseFeature = -> Pocket908
  Size = 0.2
FEATURE [PartDesign::Body] Body778  label="M3x154"
  Group = -> [Sketch2589,Pad1160,Sketch2588,Pad1161,Sketch2587,Pocket908,Chamfer590]
  Origin = -> Origin1105
  Placement = pos=(-9.3e-15,20.05,76.2) rot=(0,1,0;3.14159rad)
  Tip = -> Chamfer590
FEATURE [App::Part] Part306  label="Head_Cover_Screws"
  Group = -> [Body775,Body776,Body777,Body778]
  Origin = -> Origin1106
  Placement = pos=(1,-104.5,165.6) rot=(0,0,1;0rad)
FEATURE [Sketcher::SketchObject] Sketch2591
  MapMode = 5
  Support = -> [XY_Plane1112]
  sketch-geometry (8):
    g0: LineSegment StartX=0 StartY=2.3094 StartZ=0 EndX=-2 EndY=1.1547 EndZ=0
    g1: LineSegment StartX=-2 StartY=1.1547 StartZ=0 EndX=-2 EndY=-1.1547 EndZ=0
    g2: LineSegment StartX=-2 StartY=-1.1547 StartZ=0 EndX=-2e-16 EndY=-2.3094 EndZ=0
    g3: LineSegment StartX=-2e-16 StartY=-2.3094 StartZ=0 EndX=2 EndY=-1.1547 EndZ=0
    g4: LineSegment StartX=2 StartY=-1.1547 StartZ=0 EndX=2 EndY=1.1547 EndZ=0
    g5: LineSegment StartX=2 StartY=1.1547 StartZ=0 EndX=0 EndY=2.3094 EndZ=0
    g6: Circle [constr] CenterX=0 CenterY=0 CenterZ=0 NormalX=0 NormalY=0 NormalZ=1 AngleXU=0 Radius=2.3094
    g7: Circle CenterX=0 CenterY=0 CenterZ=0 NormalX=0 NormalY=0 NormalZ=1 AngleXU=0 Radius=1
  constraints (18):
    c: Coincident(g0,g1)
    c: Coincident(g1,g2)
    c: Coincident(g2,g3)
    c: Coincident(g3,g4)
    c: Coincident(g4,g5)
    c: Coincident(g5,g0)
    c: Equal(g0, g1-g5) x5
    c: PointOnObject(g0,g6)
    c: PointOnObject(g1,g6)
    c: PointOnObject(g2,g6)
    c: PointOnObject(g3,g6)
    c: PointOnObject(g4,g6)
    c: PointOnObject(g5,g6)
    c: Coincident(g6,g-1)
    c: PointOnObject(g5,g-2)
    c: DistanceX(g0,g4) = 4
    c: Coincident(g7,g-1)
    c: Radius(g7) = 1
FEATURE [Sketcher::SketchObject] Sketch2592
  MapMode = 5
  Support = -> [XY_Plane1112]
FEATURE [Sketcher::SketchObject] Sketch2593
  MapMode = 5
  Support = -> [XY_Plane1112]
FEATURE [Sketcher::SketchObject] Sketch2597
  MapMode = 5
  Support = -> [XY_Plane1109]
  sketch-geometry (8):
    g0: LineSegment StartX=25 StartY=10 StartZ=0 EndX=89 EndY=10 EndZ=0
    g1: LineSegment StartX=109 StartY=30 StartZ=0 EndX=109 EndY=45 EndZ=0
    g2: LineSegment StartX=84 StartY=70 StartZ=0 EndX=30 EndY=70 EndZ=0
    g3: LineSegment StartX=5 StartY=45 StartZ=0 EndX=5 EndY=30 EndZ=0
    g4: ArcOfCircle CenterX=30 CenterY=45 CenterZ=0 NormalX=0 NormalY=0 NormalZ=1 AngleXU=0 Radius=25 StartAngle=1.5708 EndAngle=3.14159
    g5: ArcOfCircle CenterX=84 CenterY=45 CenterZ=0 NormalX=0 NormalY=0 NormalZ=1 AngleXU=0 Radius=25 StartAngle=0 EndAngle=1.5708
    g6: ArcOfCircle CenterX=89 CenterY=30 CenterZ=0 NormalX=0 NormalY=0 NormalZ=1 AngleXU=0 Radius=20 StartAngle=4.71239 EndAngle=6.28319
    g7: ArcOfCircle CenterX=25 CenterY=30 CenterZ=0 NormalX=0 NormalY=0 NormalZ=1 AngleXU=0 Radius=20 StartAngle=3.14159 EndAngle=4.71239
  constraints (20):
    c: Horizontal(g0)
    c: Horizontal(g2)
    c: Vertical(g1)
    c: Vertical(g3)
    c: Tangent(g3,g4) = -1.5708
    c: Tangent(g2,g4) = -1.5708
    c: Tangent(g2,g5) = -1.5708
    c: Tangent(g1,g5) = -1.5708
    c: Tangent(g1,g6) = -1.5708
    c: Tangent(g0,g6) = -1.5708
    c: Tangent(g0,g7) = -1.5708
    c: Tangent(g3,g7) = -1.5708
    c: Equal(g4,g5)
    c: Equal(g7,g6)
    c: Radius(g5) = 25
    c: Radius(g6) = 20
    c: DistanceY(g0,g2) = 60
    c: DistanceX(g3,g1) = 104
    c: DistanceY(g-1,g0) = 10
    c: DistanceX(g-1,g3) = 5
FEATURE [Sketcher::SketchObject] Sketch2602
  AttachmentOffset = pos=(0,0,40) rot=(0,0,1;0rad)
  MapMode = 5
  Placement = pos=(0,0,40) rot=(0,0,1;0rad)
  Support = -> [XY_Plane1109]
  sketch-geometry (8):
    g0: LineSegment StartX=25 StartY=74 StartZ=0 EndX=89 EndY=74 EndZ=0
    g1: LineSegment StartX=114 StartY=49 StartZ=0 EndX=114 EndY=20 EndZ=0
    g2: LineSegment StartX=94 StartY=0 StartZ=0 EndX=20 EndY=0 EndZ=0
    g3: LineSegment StartX=0 StartY=20 StartZ=0 EndX=0 EndY=49 EndZ=0
    g4: ArcOfCircle CenterX=20 CenterY=20 CenterZ=0 NormalX=0 NormalY=0 NormalZ=1 AngleXU=0 Radius=20 StartAngle=3.14159 EndAngle=4.71239
    g5: ArcOfCircle CenterX=25 CenterY=49 CenterZ=0 NormalX=0 NormalY=0 NormalZ=1 AngleXU=0 Radius=25 StartAngle=1.5708 EndAngle=3.14159
    g6: ArcOfCircle CenterX=89 CenterY=49 CenterZ=0 NormalX=0 NormalY=0 NormalZ=1 AngleXU=0 Radius=25 StartAngle=0 EndAngle=1.5708
    g7: ArcOfCircle CenterX=94 CenterY=20 CenterZ=0 NormalX=0 NormalY=0 NormalZ=1 AngleXU=0 Radius=20 StartAngle=4.71239 EndAngle=6.28319
  constraints (20):
    c: Horizontal(g0)
    c: Horizontal(g2)
    c: Vertical(g1)
    c: Vertical(g3)
    c: Tangent(g2,g4) = 1.5708
    c: Tangent(g3,g4) = 1.5708
    c: Tangent(g3,g5) = 1.5708
    c: Tangent(g0,g5) = 1.5708
    c: Tangent(g0,g6) = 1.5708
    c: Tangent(g1,g6) = 1.5708
    c: Tangent(g1,g7) = 1.5708
    c: Tangent(g2,g7) = 1.5708
    c: Equal(g4,g7)
    c: Equal(g5,g6)
    c: Radius(g6) = 25
    c: Radius(g7) = 20
    c: PointOnObject(g2,g-1)
    c: PointOnObject(g3,g-2)
    c: DistanceX(g3,g1) = 114
    c: DistanceY(g2,g0) = 74
FEATURE [PartDesign::AdditiveLoft] AdditiveLoft  label="Baseplate048"
  Closed = false
  Profile = -> Sketch2597
  Ruled = false
  Sections = -> [Sketch2602]
FEATURE [PartDesign::Thickness] Thickness001  label="Make Shell001"
  Base = -> AdditiveLoft [Face3]
  BaseFeature = -> AdditiveLoft
  Join = 0
  Mode = 0
  Reversed = true
  Value = 2
FEATURE [PartDesign::Pad] Pad1162  label="Connection Ring"
  BaseFeature = -> Thickness001
  Length = 5
  Length2 = 100
  Profile = -> Thickness001 [Face10]
  Type = 0
FEATURE [PartDesign::Pad] Pad1163  label="Mounting Lip"
  BaseFeature = -> Pad1162
  Length = 23.75
  Length2 = 100
  Profile = -> Pad1162 [Face18]
  Type = 0
FEATURE [Sketcher::SketchObject] Sketch2596
  MapMode = 5
  Placement = pos=(0,0,0) rot=(1,0,0;1.5708rad)
  Support = -> [Pad1163]
  sketch-geometry (10):
    g0: LineSegment StartX=0 StartY=68.75 StartZ=0 EndX=32 EndY=68.75 EndZ=0
    g1: LineSegment StartX=32 StartY=68.75 StartZ=0 EndX=32 EndY=55 EndZ=0
    g2: LineSegment StartX=22 StartY=45 StartZ=0 EndX=0 EndY=45 EndZ=0
    g3: LineSegment StartX=0 StartY=45 StartZ=0 EndX=0 EndY=68.75 EndZ=0
    g4: LineSegment StartX=114 StartY=68.75 StartZ=0 EndX=82 EndY=68.75 EndZ=0
    g5: LineSegment StartX=82 StartY=68.75 StartZ=0 EndX=82 EndY=55 EndZ=0
    g6: LineSegment StartX=92 StartY=45 StartZ=0 EndX=114 EndY=45 EndZ=0
    g7: LineSegment StartX=114 StartY=45 StartZ=0 EndX=114 EndY=68.75 EndZ=0
    g8: ArcOfCircle CenterX=22 CenterY=55 CenterZ=0 NormalX=0 NormalY=0 NormalZ=1 AngleXU=0 Radius=10 StartAngle=4.71239 EndAngle=6.28319
    g9: ArcOfCircle CenterX=92 CenterY=55 CenterZ=0 NormalX=0 NormalY=0 NormalZ=1 AngleXU=0 Radius=10 StartAngle=3.14159 EndAngle=4.71239
  constraints (28):
    c: Coincident(g0,g1)
    c: Coincident(g2,g3)
    c: Coincident(g3,g0)
    c: Horizontal(g0)
    c: Horizontal(g2)
    c: Vertical(g1)
    c: Vertical(g3)
    c: PointOnObject(g0,g-2)
    c: Coincident(g4,g5)
    c: Coincident(g6,g7)
    c: Coincident(g7,g4)
    c: Horizontal(g4)
    c: Horizontal(g6)
    c: Vertical(g5)
    c: Vertical(g7)
    c: DistanceX(g0,g4) = 50
    c: Tangent(g2,g8) = 1.5708
    c: Tangent(g1,g8) = 1.5708
    c: Tangent(g6,g9) = -1.5708
    c: Tangent(g5,g9) = -1.5708
    c: Equal(g8,g9)
    c: Radius(g8) = 10
    c: Equal(g0,g4)
    c: DistanceX(g0,g4) = 114
    c: DistanceY(g-1,g0) = 68.75
    c: Horizontal(g4,g0)
    c: Equal(g5,g1)
    c: DistanceY(g3,g3) = 23.75
FEATURE [PartDesign::Pocket] Pocket909  label="Remove Upper Shell"
  BaseFeature = -> Pad1163
  Length = 40
  Length2 = 100
  Profile = -> Sketch2596
  Type = 0
FEATURE [Sketcher::SketchObject] Sketch2598
  MapMode = 5
  Placement = pos=(0,74,0) rot=(0,0.707107,0.707107;3.14159rad)
  Support = -> [Pocket909]
  sketch-geometry (10):
    g0: LineSegment StartX=-114 StartY=68.75 StartZ=0 EndX=-72 EndY=68.75 EndZ=0
    g1: LineSegment StartX=-72 StartY=68.75 StartZ=0 EndX=-72 EndY=55 EndZ=0
    g2: LineSegment StartX=-82 StartY=45 StartZ=0 EndX=-114 EndY=45 EndZ=0
    g3: LineSegment StartX=-114 StartY=45 StartZ=0 EndX=-114 EndY=68.75 EndZ=0
    g4: LineSegment StartX=0 StartY=68.75 StartZ=0 EndX=-42 EndY=68.75 EndZ=0
    g5: LineSegment StartX=-42 StartY=68.75 StartZ=0 EndX=-42 EndY=55 EndZ=0
    g6: LineSegment StartX=-32 StartY=45 StartZ=0 EndX=0 EndY=45 EndZ=0
    g7: LineSegment StartX=0 StartY=45 StartZ=0 EndX=0 EndY=68.75 EndZ=0
    g8: ArcOfCircle CenterX=-82 CenterY=55 CenterZ=0 NormalX=0 NormalY=0 NormalZ=1 AngleXU=0 Radius=10 StartAngle=4.71239 EndAngle=6.28319
    g9: ArcOfCircle CenterX=-32 CenterY=55 CenterZ=0 NormalX=0 NormalY=0 NormalZ=1 AngleXU=0 Radius=10 StartAngle=3.14159 EndAngle=4.71239
  constraints (28):
    c: Coincident(g0,g1)
    c: Coincident(g2,g3)
    c: Coincident(g3,g0)
    c: Horizontal(g0)
    c: Horizontal(g2)
    c: Vertical(g1)
    c: Vertical(g3)
    c: Coincident(g4,g5)
    c: Coincident(g6,g7)
    c: Coincident(g7,g4)
    c: Horizontal(g4)
    c: Horizontal(g6)
    c: Vertical(g5)
    c: Vertical(g7)
    c: PointOnObject(g4,g-2)
    c: DistanceX(g0,g4) = 30
    c: Tangent(g2,g8) = 1.5708
    c: Tangent(g1,g8) = 1.5708
    c: Tangent(g5,g9) = -1.5708
    c: Tangent(g6,g9) = -1.5708
    c: Equal(g9,g8)
    c: Radius(g9) = 10
    c: Horizontal(g4,g0)
    c: Equal(g1,g5)
    c: Equal(g4,g0)
    c: DistanceX(g0,g4) = 114
    c: DistanceY(g-1,g4) = 68.75
    c: DistanceY(g7,g7) = 23.75
FEATURE [PartDesign::Pocket] Pocket913  label="Remove Bottom Shell"
  BaseFeature = -> Pocket909
  Length = 40
  Length2 = 100
  Profile = -> Sketch2598
  Type = 0
FEATURE [PartDesign::Fillet] Fillet268  label="Round Shell Corners"
  Base = -> Pocket913 [Edge94,Edge114,Edge113,Edge95]
  BaseFeature = -> Pocket913
  Radius = 5
FEATURE [Sketcher::SketchObject] Sketch2600
  MapMode = 5
  Placement = pos=(0,74,0) rot=(0,0.707107,0.707107;3.14159rad)
  Support = -> [Fillet268]
  sketch-geometry (2):
    g0: Circle CenterX=-62 CenterY=63.75 CenterZ=0 NormalX=0 NormalY=0 NormalZ=1 AngleXU=0 Radius=1.6
    g1: Circle CenterX=-52 CenterY=63.75 CenterZ=0 NormalX=0 NormalY=0 NormalZ=1 AngleXU=0 Radius=1.6
  constraints (6):
    c: DistanceX(g0,g1) = 10
    c: Horizontal(g0,g1)
    c: DistanceY(g-1,g1) = 63.75
    c: DistanceX(g1,g-1) = 52
    c: Equal(g1,g0)
    c: Radius(g1) = 1.6
FEATURE [PartDesign::Pocket] Pocket910  label="Bottom Screwholes"
  BaseFeature = -> Fillet268
  Length = 5
  Length2 = 100
  Profile = -> Sketch2600
  Type = 0
FEATURE [Sketcher::SketchObject] Sketch2603
  MapMode = 5
  Placement = pos=(0,0,0) rot=(1,0,0;1.5708rad)
  Support = -> [Pocket910]
  sketch-geometry (2):
    g0: Circle CenterX=42 CenterY=63.75 CenterZ=0 NormalX=0 NormalY=0 NormalZ=1 AngleXU=0 Radius=1.6
    g1: Circle CenterX=72 CenterY=63.75 CenterZ=0 NormalX=0 NormalY=0 NormalZ=1 AngleXU=0 Radius=1.6
  constraints (6):
    c: DistanceX(g0,g1) = 30
    c: Horizontal(g1,g0)
    c: Equal(g0,g1)
    c: Radius(g1) = 1.6
    c: DistanceY(g-1,g0) = 63.75
    c: DistanceX(g-1,g0) = 42
FEATURE [PartDesign::Pocket] Pocket911  label="Top Screwholes"
  BaseFeature = -> Pocket910
  Length = 5
  Length2 = 100
  Profile = -> Sketch2603
  Type = 0
FEATURE [Sketcher::SketchObject] Sketch2599
  MapMode = 5
  Placement = pos=(0,0,2) rot=(0,0,1;0rad)
  Support = -> [Pocket911]
  sketch-geometry (6):
    g0: LineSegment StartX=19 StartY=55 StartZ=0 EndX=56 EndY=55 EndZ=0
    g1: LineSegment StartX=56 StartY=55 StartZ=0 EndX=56 EndY=25 EndZ=0
    g2: LineSegment StartX=56 StartY=25 StartZ=0 EndX=19 EndY=25 EndZ=0
    g3: LineSegment StartX=19 StartY=25 StartZ=0 EndX=19 EndY=55 EndZ=0
    g4: Circle CenterX=87 CenterY=40 CenterZ=0 NormalX=0 NormalY=0 NormalZ=1 AngleXU=0 Radius=9.75
    g5: LineSegment [constr] StartX=87 StartY=40 StartZ=0 EndX=19 EndY=40 EndZ=0
  constraints (17):
    c: Coincident(g0,g1)
    c: Coincident(g1,g2)
    c: Coincident(g2,g3)
    c: Coincident(g3,g0)
    c: Horizontal(g0)
    c: Horizontal(g2)
    c: Vertical(g1)
    c: Vertical(g3)
    c: DistanceX(g0,g0) = 37
    c: DistanceY(g3,g3) = 30
    c: Radius(g4) = 9.75
    c: Coincident(g5,g4)
    c: PointOnObject(g5,g3)
    c: Symmetric(g0,g1,g5)
    c: DistanceX(g-1,g1) = 56
    c: DistanceX(g-1,g4) = 87
    c: DistanceY(g-1,g5) = 40
FEATURE [PartDesign::Pocket] Pocket912  label="Display and Power Switch"
  BaseFeature = -> Pocket911
  Length = 5
  Length2 = 100
  Profile = -> Sketch2599
  Type = 0
FEATURE [PartDesign::Fillet] Fillet269  label="Smooth Display Corners"
  Base = -> Pocket912 [Edge125,Edge130,Edge128,Edge126]
  BaseFeature = -> Pocket912
  Radius = 0.4
FEATURE [Sketcher::SketchObject] Sketch2601
  MapMode = 5
  Placement = pos=(0,0,2) rot=(0,0,1;0rad)
  Support = -> [Fillet269]
  sketch-geometry (8):
    g0: LineSegment StartX=12 StartY=58.5 StartZ=0 EndX=67 EndY=58.5 EndZ=0
    g1: LineSegment StartX=68 StartY=57.5 StartZ=0 EndX=68 EndY=22.5 EndZ=0
    g2: LineSegment StartX=67 StartY=21.5 StartZ=0 EndX=12 EndY=21.5 EndZ=0
    g3: LineSegment StartX=11 StartY=22.5 StartZ=0 EndX=11 EndY=57.5 EndZ=0
    g4: ArcOfCircle CenterX=12 CenterY=57.5 CenterZ=0 NormalX=0 NormalY=0 NormalZ=1 AngleXU=0 Radius=1 StartAngle=1.5708 EndAngle=3.14159
    g5: ArcOfCircle CenterX=67 CenterY=57.5 CenterZ=0 NormalX=0 NormalY=0 NormalZ=1 AngleXU=0 Radius=1 StartAngle=-1.8e-15 EndAngle=1.5708
    g6: ArcOfCircle CenterX=67 CenterY=22.5 CenterZ=0 NormalX=0 NormalY=0 NormalZ=1 AngleXU=0 Radius=1 StartAngle=4.71239 EndAngle=6.28319
    g7: ArcOfCircle CenterX=12 CenterY=22.5 CenterZ=0 NormalX=0 NormalY=0 NormalZ=1 AngleXU=0 Radius=1 StartAngle=3.14159 EndAngle=4.71239
  constraints (20):
    c: Horizontal(g0)
    c: Horizontal(g2)
    c: Vertical(g1)
    c: Vertical(g3)
    c: Tangent(g3,g4) = 1.5708
    c: Tangent(g0,g4) = 1.5708
    c: Tangent(g0,g5) = 1.5708
    c: Tangent(g1,g5) = 1.5708
    c: Tangent(g1,g6) = 1.5708
    c: Tangent(g2,g6) = 1.5708
    c: Tangent(g2,g7) = 1.5708
    c: Tangent(g3,g7) = 1.5708
    c: Equal(g4,g5)
    c: Equal(g5,g6)
    c: Equal(g6,g7)
    c: Radius(g5) = 1
    c: DistanceX(g3,g1) = 57
    c: DistanceY(g2,g0) = 37
    c: DistanceY(g-1,g2) = 21.5
    c: DistanceX(g-1,g3) = 11
FEATURE [PartDesign::Pad] Pad1164  label="TFT PCB Base"
  BaseFeature = -> Fillet269
  Length = 4.5
  Length2 = 100
  Profile = -> Sketch2601
  Type = 0
FEATURE [Sketcher::SketchObject] Sketch2595
  MapMode = 5
  Placement = pos=(0,0,6.5) rot=(0,0,1;0rad)
  Support = -> [Pad1164]
  sketch-geometry (4):
    g0: LineSegment StartX=12.25 StartY=22.75 StartZ=0 EndX=66.75 EndY=22.75 EndZ=0
    g1: LineSegment StartX=66.75 StartY=22.75 StartZ=0 EndX=66.75 EndY=57.25 EndZ=0
    g2: LineSegment StartX=66.75 StartY=57.25 StartZ=0 EndX=12.25 EndY=57.25 EndZ=0
    g3: LineSegment StartX=12.25 StartY=57.25 StartZ=0 EndX=12.25 EndY=22.75 EndZ=0
  constraints (12):
    c: Coincident(g0,g1)
    c: Coincident(g1,g2)
    c: Coincident(g2,g3)
    c: Coincident(g3,g0)
    c: Horizontal(g0)
    c: Horizontal(g2)
    c: Vertical(g1)
    c: Vertical(g3)
    c: DistanceX(g2,g2) = 54.5
    c: DistanceY(g3,g3) = 34.5
    c: DistanceY(g-1,g0) = 22.75
    c: DistanceX(g-1,g0) = 12.25
FEATURE [PartDesign::Pocket] Pocket914  label="TFT PCB Pocket"
  BaseFeature = -> Pad1164
  Length = 1.5
  Length2 = 100
  Profile = -> Sketch2595
  Type = 0
FEATURE [PartDesign::Fillet] Fillet270  label="TFT PCB Pocket Fillet"
  Base = -> Pocket914 [Edge216,Edge219,Edge221,Edge217]
  BaseFeature = -> Pocket914
  Radius = 0.4
FEATURE [Sketcher::SketchObject] Sketch2604
  MapMode = 5
  Placement = pos=(0,0,5) rot=(0,0,1;0rad)
  Support = -> [Fillet270]
  sketch-geometry (12):
    g0: LineSegment StartX=17.25 StartY=57.25 StartZ=0 EndX=61.75 EndY=57.25 EndZ=0
    g1: LineSegment StartX=61.75 StartY=57.25 StartZ=0 EndX=61.75 EndY=52.25 EndZ=0
    g2: LineSegment StartX=61.75 StartY=22.75 StartZ=0 EndX=17.25 EndY=22.75 EndZ=0
    g3: LineSegment StartX=17.25 StartY=22.75 StartZ=0 EndX=17.25 EndY=27.75 EndZ=0
    g4: LineSegment StartX=12.25 StartY=52.25 StartZ=0 EndX=17.25 EndY=52.25 EndZ=0
    g5: LineSegment StartX=66.75 StartY=52.25 StartZ=0 EndX=66.75 EndY=27.75 EndZ=0
    g6: LineSegment StartX=66.75 StartY=27.75 StartZ=0 EndX=61.75 EndY=27.75 EndZ=0
    g7: LineSegment StartX=12.25 StartY=27.75 StartZ=0 EndX=12.25 EndY=52.25 EndZ=0
    g8: LineSegment StartX=17.25 StartY=52.25 StartZ=0 EndX=17.25 EndY=57.25 EndZ=0
    g9: LineSegment StartX=61.75 StartY=52.25 StartZ=0 EndX=66.75 EndY=52.25 EndZ=0
    g10: LineSegment StartX=61.75 StartY=27.75 StartZ=0 EndX=61.75 EndY=22.75 EndZ=0
    g11: LineSegment StartX=17.25 StartY=27.75 StartZ=0 EndX=12.25 EndY=27.75 EndZ=0
  constraints (32):
    c: Coincident(g0,g1)
    c: Coincident(g10,g2)
    c: Coincident(g2,g3)
    c: Coincident(g8,g0)
    c: Horizontal(g0)
    c: Horizontal(g2)
    c: Vertical(g1)
    c: Vertical(g3)
    c: DistanceX(g0,g0) = 44.5
    c: DistanceY(g3,g8) = 34.5
    c: DistanceX(g-1,g2) = 17.25
    c: DistanceY(g-1,g2) = 22.75
    c: Coincident(g9,g5)
    c: Coincident(g5,g6)
    c: Coincident(g11,g7)
    c: Coincident(g7,g4)
    c: Tangent(g3,g8)
    c: Coincident(g4,g8)
    c: Tangent(g4,g9)
    c: Coincident(g1,g9)
    c: Tangent(g1,g10)
    c: Coincident(g6,g10)
    c: Coincident(g11,g3)
    c: Tangent(g6,g11)
    c: Equal(g11,g4)
    c: Equal(g4,g9)
    c: Equal(g9,g6)
    c: Equal(g6,g1)
    c: Equal(g1,g8)
    c: Equal(g8,g3)
    c: Equal(g3,g10)
    c: DistanceX(g4,g5) = 54.5
FEATURE [PartDesign::Pocket] Pocket915  label="TFT Screen Pocket"
  BaseFeature = -> Fillet270
  Length = 3
  Length2 = 100
  Profile = -> Sketch2604
  Type = 0
FEATURE [Sketcher::SketchObject] Sketch2605
  MapMode = 5
  Placement = pos=(0,0,5) rot=(0,0,1;0rad)
  Support = -> [Pocket915]
  sketch-geometry (4):
    g0: Circle CenterX=14.5 CenterY=55 CenterZ=0 NormalX=0 NormalY=0 NormalZ=1 AngleXU=0 Radius=0.95
    g1: Circle CenterX=64.5 CenterY=55 CenterZ=0 NormalX=0 NormalY=0 NormalZ=1 AngleXU=0 Radius=0.95
    g2: Circle CenterX=64.5 CenterY=25 CenterZ=0 NormalX=0 NormalY=0 NormalZ=1 AngleXU=0 Radius=0.95
    g3: Circle CenterX=14.5 CenterY=25 CenterZ=0 NormalX=0 NormalY=0 NormalZ=1 AngleXU=0 Radius=0.95
  constraints (12):
    c: Horizontal(g0,g1)
    c: Horizontal(g3,g2)
    c: Vertical(g3,g0)
    c: Vertical(g2,g1)
    c: DistanceX(g0,g1) = 50
    c: DistanceY(g3,g0) = 30
    c: DistanceX(g-1,g3) = 14.5
    c: DistanceY(g-1,g3) = 25
    c: Equal(g3,g0)
    c: Equal(g0,g1)
    c: Equal(g1,g2)
    c: Radius(g0) = 0.95
FEATURE [PartDesign::Pocket] Pocket916  label="TFT Screwholes"
  BaseFeature = -> Pocket915
  Length = 5
  Length2 = 100
  Profile = -> Sketch2605
  Type = 0
FEATURE [PartDesign::Body] Body785  label="Rear_Cover"
  Group = -> [Sketch2602,Sketch2597,AdditiveLoft,Thickness001,Pad1162,Pad1163,Sketch2596,Pocket909,Sketch2598,Pocket913,Fillet268,Sketch2600,Pocket910,Sketch2603,Pocket911,Sketch2599,Pocket912,Fillet269,Sketch2601,Pad1164,Sketch2595,Pocket914,Fillet270,Sketch2604,Pocket915,Sketch2605,Pocket916]
  Origin = -> Origin1107
  Tip = -> Pocket916
FEATURE [Sketcher::SketchObject] Sketch2607
  MapMode = 5
  Support = -> [XY_Plane1110]
  sketch-geometry (1):
    g0: Circle CenterX=0 CenterY=0 CenterZ=0 NormalX=0 NormalY=0 NormalZ=1 AngleXU=0 Radius=1.9
  constraints (2):
    c: Coincident(g0,g-1)
    c: Radius(g0) = 1.9
FEATURE [Sketcher::SketchObject] Sketch2609
  MapMode = 5
  Support = -> [XY_Plane1124]
  sketch-geometry (8):
    g0: Circle CenterX=0 CenterY=0 CenterZ=0 NormalX=0 NormalY=0 NormalZ=1 AngleXU=0 Radius=9.625
    g1: LineSegment StartX=0 StartY=12.7 StartZ=0 EndX=-10.9985 EndY=6.35 EndZ=0
    g2: LineSegment StartX=-10.9985 StartY=6.35 StartZ=0 EndX=-10.9985 EndY=-6.35 EndZ=0
    g3: LineSegment StartX=-10.9985 StartY=-6.35 StartZ=0 EndX=0 EndY=-12.7 EndZ=0
    g4: LineSegment StartX=0 StartY=-12.7 StartZ=0 EndX=10.9985 EndY=-6.35 EndZ=0
    g5: LineSegment StartX=10.9985 StartY=-6.35 StartZ=0 EndX=10.9985 EndY=6.35 EndZ=0
    g6: LineSegment StartX=10.9985 StartY=6.35 StartZ=0 EndX=0 EndY=12.7 EndZ=0
    g7: Circle [constr] CenterX=0 CenterY=0 CenterZ=0 NormalX=0 NormalY=0 NormalZ=1 AngleXU=0 Radius=12.7
  constraints (18):
    c: Coincident(g0,g-1)
    c: Coincident(g1,g2)
    c: Coincident(g2,g3)
    c: Coincident(g3,g4)
    c: Coincident(g4,g5)
    c: Coincident(g5,g6)
    c: Coincident(g6,g1)
    c: Equal(g1, g2-g6) x5
    c: PointOnObject(g1,g7)
    c: PointOnObject(g2,g7)
    c: PointOnObject(g3,g7)
    c: PointOnObject(g4,g7)
    c: PointOnObject(g5,g7)
    c: PointOnObject(g6,g7)
    c: Coincident(g7,g0)
    c: PointOnObject(g1,g-2)
    c: DistanceY(g3,g1) = 25.4
    c: Radius(g0) = 9.625
FEATURE [Sketcher::SketchObject] Sketch2610
  MapMode = 5
  Placement = pos=(0,0,0) rot=(0.57735,0.57735,0.57735;2.0944rad)
  Support = -> [YZ_Plane1115]
  sketch-geometry (7):
    g0: LineSegment StartX=9.5 StartY=3.5 StartZ=0 EndX=12.75 EndY=2.25 EndZ=0
    g1: LineSegment StartX=12.75 StartY=2.25 StartZ=0 EndX=12.75 EndY=0.75 EndZ=0
    g2: LineSegment StartX=12.75 StartY=0.75 StartZ=0 EndX=9.5 EndY=-0.5 EndZ=0
    g3: LineSegment StartX=9.5 StartY=-0.5 StartZ=0 EndX=14.5 EndY=-0.5 EndZ=0
    g4: LineSegment StartX=14.5 StartY=-0.5 StartZ=0 EndX=14.5 EndY=3.5 EndZ=0
    g5: LineSegment StartX=14.5 StartY=3.5 StartZ=0 EndX=9.5 EndY=3.5 EndZ=0
    g6: LineSegment [constr] StartX=12.75 StartY=1.5 StartZ=0 EndX=14.5 EndY=1.5 EndZ=0
  constraints (20):
    c: Coincident(g0,g1)
    c: Vertical(g1)
    c: Coincident(g1,g2)
    c: Coincident(g2,g3)
    c: Coincident(g3,g4)
    c: Vertical(g4)
    c: Coincident(g4,g5)
    c: Coincident(g5,g0)
    c: Horizontal(g5)
    c: DistanceY(g4,g4) = 4
    c: PointOnObject(g6,g1)
    c: Symmetric(g4,g3,g6)
    c: Symmetric(g0,g1,g6)
    c: Vertical(g2,g0)
    c: DistanceX(g-1,g2) = 9.5
    c: DistanceX(g2,g1) = 3.25
    c: DistanceX(g5,g5) = 5
    c: DistanceY(g1,g1) = 1.5
    c: Horizontal(g3)
    c: DistanceY(g2,g-1) = 0.5
FEATURE [Sketcher::SketchObject] Sketch2611
  MapMode = 5
  Placement = pos=(0,0,0) rot=(1,0,0;1.5708rad)
  Support = -> [XZ_Plane1121]
  sketch-geometry (14):
    g0: LineSegment StartX=0 StartY=22 StartZ=0 EndX=6.5 EndY=22 EndZ=0
    g1: LineSegment StartX=6.5 StartY=22 StartZ=0 EndX=6.5 EndY=20 EndZ=0
    g2: LineSegment StartX=6.5 StartY=20 StartZ=0 EndX=8.5 EndY=20 EndZ=0
    g3: LineSegment StartX=8.5 StartY=20 StartZ=0 EndX=8.5 EndY=22 EndZ=0
    g4: LineSegment StartX=8.5 StartY=22 StartZ=0 EndX=9.5 EndY=22 EndZ=0
    g5: LineSegment StartX=9.5 StartY=22 StartZ=0 EndX=11 EndY=20.5 EndZ=0
    g6: LineSegment StartX=11 StartY=20.5 StartZ=0 EndX=11 EndY=20 EndZ=0
    g7: LineSegment StartX=11 StartY=20 StartZ=0 EndX=9.5 EndY=20 EndZ=0
    g8: LineSegment StartX=9.5 StartY=20 StartZ=0 EndX=9.5 EndY=0 EndZ=0
    g9: LineSegment StartX=0 StartY=0 StartZ=0 EndX=0 EndY=22 EndZ=0
    g10: LineSegment StartX=9.5 StartY=0 StartZ=0 EndX=7.5 EndY=0 EndZ=0
    g11: LineSegment StartX=7.5 StartY=0 StartZ=0 EndX=7.5 EndY=-10 EndZ=0
    g12: LineSegment StartX=7.5 StartY=-10 StartZ=0 EndX=0 EndY=-10 EndZ=0
    g13: LineSegment StartX=0 StartY=-10 StartZ=0 EndX=0 EndY=0 EndZ=0
  constraints (41):
    c: PointOnObject(g0,g-2)
    c: Horizontal(g0)
    c: Coincident(g0,g1)
    c: Coincident(g1,g2)
    c: Horizontal(g2)
    c: Coincident(g2,g3)
    c: Coincident(g3,g4)
    c: Coincident(g4,g5)
    c: Coincident(g5,g6)
    c: Vertical(g6)
    c: Coincident(g6,g7)
    c: Horizontal(g7)
    c: Coincident(g7,g8)
    c: Vertical(g8)
    c: Coincident(g9,g0)
    c: Horizontal(g0,g3)
    c: Horizontal(g4)
    c: Vertical(g4,g7)
    c: DistanceY(g7,g4) = 2
    c: DistanceX(g0,g5) = 11
    c: DistanceX(g0,g4) = 9.5
    c: Vertical(g3)
    c: Vertical(g1)
    c: DistanceY(g6,g6) = 0.5
    c: DistanceY(g8,g8) = 20
    c: Horizontal(g2,g7)
    c: DistanceX(g4,g4) = 1
    c: DistanceX(g2,g2) = 2
    c: Coincident(g8,g10)
    c: Horizontal(g10)
    c: Coincident(g10,g11)
    c: Vertical(g11)
    c: Coincident(g11,g12)
    c: PointOnObject(g12,g-2)
    c: Horizontal(g12)
    c: Coincident(g12,g13)
    c: Coincident(g13,g9)
    c: DistanceX(g12,g12) = 7.5
    c: DistanceY(g11,g11) = 10
    c: PointOnObject(g10,g-1)
    c: Coincident(g9,g-1)
FEATURE [Sketcher::SketchObject] Sketch2614
  MapMode = 5
  Placement = pos=(0,0,0) rot=(1,0,0;1.5708rad)
  Support = -> [XZ_Plane1116]
  sketch-geometry (4):
    g0: LineSegment StartX=6.55 StartY=22 StartZ=0 EndX=8.45 EndY=22 EndZ=0
    g1: LineSegment StartX=8.45 StartY=22 StartZ=0 EndX=8.45 EndY=20 EndZ=0
    g2: LineSegment StartX=8.45 StartY=20 StartZ=0 EndX=6.55 EndY=20 EndZ=0
    g3: LineSegment StartX=6.55 StartY=20 StartZ=0 EndX=6.55 EndY=22 EndZ=0
  constraints (12):
    c: Coincident(g0,g1)
    c: Coincident(g1,g2)
    c: Coincident(g2,g3)
    c: Coincident(g3,g0)
    c: Horizontal(g0)
    c: Horizontal(g2)
    c: Vertical(g1)
    c: Vertical(g3)
    c: DistanceX(g0,g0) = 1.9
    c: DistanceX(g-1,g0) = 6.55
    c: DistanceY(g3,g3) = 2
    c: DistanceY(g-1,g2) = 20
FEATURE [PartDesign::Revolution] Revolution058
  Angle = 360
  Axis = (0,2e-16,1)
  Base = (0,0,0)
  Placement = pos=(0,0,0) rot=(1,0,0;1.5708rad)
  Profile = -> Sketch2611
  ReferenceAxis = -> Sketch2611 [V_Axis]
  Reversed = true
FEATURE [PartDesign::Pad] Pad1170
  Length = 3
  Length2 = 100
  Profile = -> Sketch2609
  Type = 0
FEATURE [PartDesign::Revolution] Revolution059
  Angle = 360
  Axis = (0,2e-16,1)
  Base = (0,0,0)
  Placement = pos=(0,0,0) rot=(1,0,0;1.5708rad)
  Profile = -> Sketch2614
  ReferenceAxis = -> Sketch2614 [V_Axis]
  Reversed = true
FEATURE [PartDesign::Groove] Groove253
  Angle = 360
  Axis = (-2e-16,3e-16,1)
  Base = (0,0,0)
  BaseFeature = -> Pad1170
  Profile = -> Sketch2610
  ReferenceAxis = -> Sketch2610 [V_Axis]
FEATURE [PartDesign::Body] Body793  label="Push Button Nut"
  Group = -> [Sketch2609,Pad1170,Sketch2610,Groove253]
  Origin = -> Origin1125
  Placement = pos=(0,0,15) rot=(0,0,1;0rad)
  Tip = -> Groove253
FEATURE [PartDesign::Pad] Pad1176  label="M3 Nut Primitive246"
  Length = 0.6
  Length2 = 0.6
  Profile = -> Sketch2591
  Type = 4
FEATURE [Sketcher::SketchObject] Sketch2594
  ExternalGeometry = -> [Pad1176]
  MapMode = 5
  Placement = pos=(0,0,0) rot=(0.57735,0.57735,0.57735;2.0944rad)
  Support = -> [YZ_Plane1109]
  sketch-geometry (6):
    g0: LineSegment StartX=-1.9594 StartY=0.6 StartZ=0 EndX=-2.8094 EndY=0.6 EndZ=0
    g1: LineSegment StartX=-2.8094 StartY=0.6 StartZ=0 EndX=-2.8094 EndY=-0.6 EndZ=0
    g2: LineSegment StartX=-2.8094 StartY=-0.6 StartZ=0 EndX=-1.9594 EndY=-0.6 EndZ=0
    g3: LineSegment StartX=-1.9594 StartY=-0.6 StartZ=0 EndX=-2.3094 EndY=-0.4 EndZ=0
    g4: LineSegment StartX=-2.3094 StartY=-0.4 StartZ=0 EndX=-2.3094 EndY=0.4 EndZ=0
    g5: LineSegment StartX=-2.3094 StartY=0.4 StartZ=0 EndX=-1.9594 EndY=0.6 EndZ=0
  constraints (15):
    c: Horizontal(g0)
    c: Coincident(g0,g1)
    c: Coincident(g1,g2)
    c: Coincident(g2,g3)
    c: Coincident(g3,g4)
    c: Coincident(g4,g5)
    c: Coincident(g5,g0)
    c: Symmetric(g4,g3,g-1)
    c: Symmetric(g0,g2,g-1)
    c: Symmetric(g1,g0,g-1)
    c: DistanceX(g0,g4) = 0.5
    c: DistanceY(g3,g4) = 0.8
    c: DistanceY(g1,g0) = 1.2
    c: PointOnObject(g3,g-3)
    c: DistanceX(g4,g0) = 0.35
FEATURE [PartDesign::Groove] Groove254  label="M3 Nut Smooth245"
  Angle = 360
  Axis = (-2e-16,3e-16,1)
  Base = (0,0,0)
  BaseFeature = -> Pad1176
  Profile = -> Sketch2594
  ReferenceAxis = -> Sketch2594 [V_Axis]
  Reversed = true
FEATURE [PartDesign::Chamfer] Chamfer595  label="M3 Nut Smooth Hole245"
  Base = -> Groove254 [Edge24,Edge23]
  BaseFeature = -> Groove254
  Size = 0.2
FEATURE [PartDesign::Body] Body784  label="M2 Nut003"
  Group = -> [Sketch2591,Pad1176,Sketch2594,Groove254,Chamfer595,Sketch2592,Sketch2593]
  Origin = -> Origin1109
  Placement = pos=(64.5,55,0) rot=(0,0,1;0rad)
  Tip = -> Chamfer595
FEATURE [PartDesign::Pad] Pad1180  label="M3x8 Head185"
  Length = 2
  Length2 = 100
  Profile = -> Sketch2607
  Type = 0
FEATURE [Sketcher::SketchObject] Sketch2608
  MapMode = 5
  Placement = pos=(0,0,2) rot=(0,0,1;0rad)
  Support = -> [Pad1180]
  sketch-geometry (1):
    g0: Circle CenterX=0 CenterY=0 CenterZ=0 NormalX=0 NormalY=0 NormalZ=1 AngleXU=0 Radius=1
  constraints (2):
    c: Coincident(g0,g-1)
    c: Radius(g0) = 1
FEATURE [PartDesign::Pad] Pad1179  label="M3x8 Thread185"
  BaseFeature = -> Pad1180
  Length = 8
  Length2 = 100
  Profile = -> Sketch2608
  Type = 0
FEATURE [Sketcher::SketchObject] Sketch2606
  MapMode = 5
  Placement = pos=(0,0,0) rot=(1,0,0;3.14159rad)
  Support = -> [Pad1179]
  sketch-geometry (7):
    g0: LineSegment StartX=0.77 StartY=0.44456 StartZ=0 EndX=0 EndY=0.889119 EndZ=0
    g1: LineSegment StartX=0 StartY=0.889119 StartZ=0 EndX=-0.77 EndY=0.44456 EndZ=0
    g2: LineSegment StartX=-0.77 StartY=0.44456 StartZ=0 EndX=-0.77 EndY=-0.44456 EndZ=0
    g3: LineSegment StartX=-0.77 StartY=-0.44456 StartZ=0 EndX=3.85628e-11 EndY=-0.889119 EndZ=0
    g4: LineSegment StartX=3.85628e-11 StartY=-0.889119 StartZ=0 EndX=0.77 EndY=-0.44456 EndZ=0
    g5: LineSegment StartX=0.77 StartY=-0.44456 StartZ=0 EndX=0.77 EndY=0.44456 EndZ=0
    g6: Circle [constr] CenterX=0 CenterY=0 CenterZ=0 NormalX=0 NormalY=0 NormalZ=1 AngleXU=0 Radius=0.889119
  constraints (16):
    c: Coincident(g0,g1)
    c: Coincident(g1,g2)
    c: Coincident(g2,g3)
    c: Coincident(g3,g4)
    c: Coincident(g4,g5)
    c: Coincident(g5,g0)
    c: Equal(g0, g1-g5) x5
    c: PointOnObject(g0,g6)
    c: PointOnObject(g1,g6)
    c: PointOnObject(g2,g6)
    c: PointOnObject(g3,g6)
    c: PointOnObject(g4,g6)
    c: PointOnObject(g5,g6)
    c: Coincident(g6,g-1)
    c: PointOnObject(g0,g-2)
    c: DistanceX(g1,g0) = 1.54
FEATURE [PartDesign::Pocket] Pocket920  label="M3x8 Wrench184"
  BaseFeature = -> Pad1179
  Length = 1
  Length2 = 100
  Profile = -> Sketch2606
  Type = 0
FEATURE [PartDesign::Chamfer] Chamfer596  label="M3x8 Smooth182"
  Base = -> Pocket920 [Face11,Edge2,Edge24,Edge3]
  BaseFeature = -> Pocket920
  Size = 0.2
FEATURE [Sketcher::SketchObject] Sketch2615
  MapMode = 5
  Placement = pos=(0,0,0) rot=(1,0,0;1.5708rad)
  Support = -> [XZ_Plane1103]
  sketch-geometry (4):
    g0: LineSegment StartX=-0.32 StartY=-3 StartZ=0 EndX=0.32 EndY=-3 EndZ=0
    g1: LineSegment StartX=0.32 StartY=-3 StartZ=0 EndX=0.32 EndY=8.54 EndZ=0
    g2: LineSegment StartX=0.32 StartY=8.54 StartZ=0 EndX=-0.32 EndY=8.54 EndZ=0
    g3: LineSegment StartX=-0.32 StartY=8.54 StartZ=0 EndX=-0.32 EndY=-3 EndZ=0
  constraints (11):
    c: Coincident(g0,g1)
    c: Coincident(g1,g2)
    c: Coincident(g2,g3)
    c: Coincident(g3,g0)
    c: Horizontal(g0)
    c: Vertical(g1)
    c: Vertical(g3)
    c: DistanceY(g-1,g1) = 8.54
    c: DistanceY(g0,g-1) = 3
    c: Symmetric(g2,g1,g-2)
    c: DistanceX(g2,g2) = 0.64
FEATURE [PartDesign::Pad] Pad1165
  Length = 0.32
  Length2 = 0.32
  Placement = pos=(0,0,0) rot=(1,0,0;1.5708rad)
  Profile = -> Sketch2615
  Type = 4
FEATURE [PartDesign::Chamfer] Chamfer594
  Base = -> Pad1165 [Face3,Face1]
  BaseFeature = -> Pad1165
  Placement = pos=(0,0,0) rot=(1,0,0;1.5708rad)
  Size = 0.16
FEATURE [PartDesign::Body] Body780  label="Pin Header Pin004"
  Group = -> [Sketch2615,Pad1165,Chamfer594]
  Origin = -> Origin1128
  Tip = -> Chamfer594
FEATURE [Part::FeaturePython] Array007  # Draft array (typed FeaturePython)
  Angle = 360
  ArrayType = 0
  Axis = (0,0,1)
  Base = -> Body780
  Center = (0,0,0)
  Fuse = false
  IntervalAxis = (0,0,0)
  IntervalX = (1,0,0)
  IntervalY = (0,2.54,0)
  IntervalZ = (0,0,1)
  NumberPolar = 1
  NumberX = 1
  NumberY = 8
  NumberZ = 1
FEATURE [Sketcher::SketchObject] Sketch2616
  MapMode = 5
  Support = -> [XY_Plane1106]
  sketch-geometry (4):
    g0: LineSegment StartX=-1.27 StartY=-1.27 StartZ=0 EndX=1.27 EndY=-1.27 EndZ=0
    g1: LineSegment StartX=1.27 StartY=-1.27 StartZ=0 EndX=1.27 EndY=1.27 EndZ=0
    g2: LineSegment StartX=1.27 StartY=1.27 StartZ=0 EndX=-1.27 EndY=1.27 EndZ=0
    g3: LineSegment StartX=-1.27 StartY=1.27 StartZ=0 EndX=-1.27 EndY=-1.27 EndZ=0
  constraints (10):
    c: Coincident(g0,g1)
    c: Coincident(g1,g2)
    c: Coincident(g2,g3)
    c: Coincident(g3,g0)
    c: Horizontal(g0)
    c: Vertical(g3)
    c: Symmetric(g1,g2,g-2)
    c: Symmetric(g0,g1,g-1)
    c: Equal(g3,g2)
    c: DistanceX(g2,g2) = 2.54
FEATURE [PartDesign::Pad] Pad1169
  Length = 2.5
  Length2 = 100
  Profile = -> Sketch2616
  Type = 0
FEATURE [PartDesign::Chamfer] Chamfer592
  Base = -> Pad1169 [Edge2,Edge1,Edge5,Edge8]
  BaseFeature = -> Pad1169
  Size = 0.2
FEATURE [PartDesign::Chamfer] Chamfer591
  Base = -> Chamfer592 [Face5,Face2]
  BaseFeature = -> Chamfer592
  Size = 0.05
FEATURE [PartDesign::Body] Body782  label="Pin Header Block004"
  Group = -> [Sketch2616,Pad1169,Chamfer592,Chamfer591]
  Origin = -> Origin1116
  Tip = -> Chamfer591
FEATURE [Part::FeaturePython] Array006  # Draft array (typed FeaturePython)
  Angle = 360
  ArrayType = 0
  Axis = (0,0,1)
  Base = -> Body782
  Center = (0,0,0)
  Fuse = false
  IntervalAxis = (0,0,0)
  IntervalX = (1,0,0)
  IntervalY = (0,2.54,0)
  IntervalZ = (0,0,1)
  NumberPolar = 1
  NumberX = 1
  NumberY = 8
  NumberZ = 1
FEATURE [App::Part] Part310  label="Pin Header004"
  Group = -> [Body782,Body780,Array006,Array007]
  Origin = -> Origin1129
  Placement = pos=(25,8.9,-1.1e-15) rot=(1,0,0;3.14159rad)
FEATURE [Sketcher::SketchObject] Sketch2617
  MapMode = 5
  Support = -> [XY_Plane1111]
  sketch-geometry (4):
    g0: LineSegment StartX=-22 StartY=17 StartZ=0 EndX=22 EndY=17 EndZ=0
    g1: LineSegment StartX=22 StartY=17 StartZ=0 EndX=22 EndY=-17 EndZ=0
    g2: LineSegment StartX=22 StartY=-17 StartZ=0 EndX=-22 EndY=-17 EndZ=0
    g3: LineSegment StartX=-22 StartY=-17 StartZ=0 EndX=-22 EndY=17 EndZ=0
  constraints (10):
    c: Coincident(g0,g1)
    c: Coincident(g1,g2)
    c: Coincident(g2,g3)
    c: Coincident(g3,g0)
    c: Horizontal(g2)
    c: Vertical(g1)
    c: Symmetric(g0,g2,g-1)
    c: DistanceX(g0,g0) = 44
    c: DistanceY(g3,g3) = 34
    c: Symmetric(g0,g0,g-2)
FEATURE [PartDesign::Pad] Pad1166
  Length = 2.25
  Length2 = 100
  Profile = -> Sketch2617
  Type = 0
FEATURE [PartDesign::Body] Body781  label="1,8" TFT Screen Frame"
  Group = -> [Sketch2617,Pad1166]
  Origin = -> Origin1119
  Placement = pos=(0,0,1.2) rot=(0,0,1;0rad)
  Tip = -> Pad1166
FEATURE [Sketcher::SketchObject] Sketch2618
  MapMode = 5
  Support = -> [XY_Plane1105]
  sketch-geometry (4):
    g0: LineSegment StartX=-16 StartY=-14.5 StartZ=0 EndX=20 EndY=-14.5 EndZ=0
    g1: LineSegment StartX=20 StartY=-14.5 StartZ=0 EndX=20 EndY=14.5 EndZ=0
    g2: LineSegment StartX=20 StartY=14.5 StartZ=0 EndX=-16 EndY=14.5 EndZ=0
    g3: LineSegment StartX=-16 StartY=14.5 StartZ=0 EndX=-16 EndY=-14.5 EndZ=0
  constraints (11):
    c: Coincident(g0,g1)
    c: Coincident(g1,g2)
    c: Coincident(g2,g3)
    c: Coincident(g3,g0)
    c: Horizontal(g0)
    c: Horizontal(g2)
    c: Vertical(g3)
    c: DistanceX(g2,g2) = 36
    c: DistanceY(g1,g1) = 29
    c: Symmetric(g1,g0,g-1)
    c: DistanceX(g-1,g0) = 20
FEATURE [PartDesign::Pad] Pad1168
  Length = 0.1
  Length2 = 100
  Profile = -> Sketch2618
  Type = 0
FEATURE [PartDesign::Body] Body783  label="1,8" TFT Screen"
  Group = -> [Sketch2618,Pad1168]
  Origin = -> Origin1123
  Placement = pos=(0,0,3.45) rot=(0,0,1;0rad)
  Tip = -> Pad1168
FEATURE [Sketcher::SketchObject] Sketch2619
  MapMode = 5
  Support = -> [XY_Plane1108]
  sketch-geometry (8):
    g0: LineSegment StartX=-27 StartY=17 StartZ=0 EndX=27 EndY=17 EndZ=0
    g1: LineSegment StartX=27 StartY=17 StartZ=0 EndX=27 EndY=-17 EndZ=0
    g2: LineSegment StartX=27 StartY=-17 StartZ=0 EndX=-27 EndY=-17 EndZ=0
    g3: LineSegment StartX=-27 StartY=-17 StartZ=0 EndX=-27 EndY=17 EndZ=0
    g4: Circle CenterX=-25 CenterY=15 CenterZ=0 NormalX=0 NormalY=0 NormalZ=1 AngleXU=0 Radius=1
    g5: Circle CenterX=25 CenterY=15 CenterZ=0 NormalX=0 NormalY=0 NormalZ=1 AngleXU=0 Radius=1
    g6: Circle CenterX=-25 CenterY=-15 CenterZ=0 NormalX=0 NormalY=0 NormalZ=1 AngleXU=0 Radius=1
    g7: Circle CenterX=25 CenterY=-15 CenterZ=0 NormalX=0 NormalY=0 NormalZ=1 AngleXU=0 Radius=1
  constraints (19):
    c: Coincident(g0,g1)
    c: Coincident(g1,g2)
    c: Coincident(g2,g3)
    c: Coincident(g3,g0)
    c: Horizontal(g2)
    c: Vertical(g3)
    c: Symmetric(g0,g0,g-2)
    c: Symmetric(g0,g1,g-1)
    c: DistanceX(g0,g0) = 54
    c: DistanceY(g1,g1) = 34
    c: Symmetric(g4,g5,g-2)
    c: Symmetric(g7,g6,g-2)
    c: Symmetric(g7,g5,g-1)
    c: Equal(g7,g5)
    c: Equal(g5,g4)
    c: Equal(g4,g6)
    c: Radius(g4) = 1
    c: DistanceY(g7,g5) = 30
    c: DistanceX(g6,g7) = 50
FEATURE [PartDesign::Pad] Pad1167
  Length = 1.2
  Length2 = 100
  Profile = -> Sketch2619
  Type = 0
FEATURE [PartDesign::Chamfer] Chamfer593
  Base = -> Pad1167 [Edge8,Edge5,Edge2,Edge1]
  BaseFeature = -> Pad1167
  Size = 1.41
FEATURE [PartDesign::Body] Body779  label="1,8" TFT PCB"
  Group = -> [Sketch2619,Pad1167,Chamfer593]
  Origin = -> Origin1127
  Tip = -> Chamfer593
FEATURE [App::Part] Part309  label="1,8" TFT"
  Group = -> [Body779,Body781,Body783,Part310]
  Origin = -> Origin1111
  Placement = pos=(39.5,40,6.35) rot=(0,1,0;3.14159rad)
FEATURE [PartDesign::Fillet] Fillet005
  Base = -> Revolution058 [Edge1,Edge5]
  BaseFeature = -> Revolution058
  Placement = pos=(0,0,0) rot=(1,0,0;1.5708rad)
  Radius = 0.15
FEATURE [Sketcher::SketchObject] Sketch2590
  MapMode = 5
  Placement = pos=(0,-6.6e-15,-10) rot=(1,0,0;3.14159rad)
  Support = -> [Fillet005]
  sketch-geometry (16):
    g0: LineSegment StartX=-1.5 StartY=5 StartZ=0 EndX=1.5 EndY=5 EndZ=0
    g1: LineSegment StartX=1.5 StartY=5 StartZ=0 EndX=1.5 EndY=5.5 EndZ=0
    g2: LineSegment StartX=1.5 StartY=5.5 StartZ=0 EndX=-1.5 EndY=5.5 EndZ=0
    g3: LineSegment StartX=-1.5 StartY=5.5 StartZ=0 EndX=-1.5 EndY=5 EndZ=0
    g4: LineSegment StartX=5 StartY=-1.5 StartZ=0 EndX=5.5 EndY=-1.5 EndZ=0
    g5: LineSegment StartX=5.5 StartY=-1.5 StartZ=0 EndX=5.5 EndY=1.5 EndZ=0
    g6: LineSegment StartX=5.5 StartY=1.5 StartZ=0 EndX=5 EndY=1.5 EndZ=0
    g7: LineSegment StartX=5 StartY=1.5 StartZ=0 EndX=5 EndY=-1.5 EndZ=0
    g8: LineSegment StartX=1.5 StartY=-5 StartZ=0 EndX=-1.5 EndY=-5 EndZ=0
    g9: LineSegment StartX=-1.5 StartY=-5 StartZ=0 EndX=-1.5 EndY=-5.5 EndZ=0
    g10: LineSegment StartX=-1.5 StartY=-5.5 StartZ=0 EndX=1.5 EndY=-5.5 EndZ=0
    g11: LineSegment StartX=1.5 StartY=-5.5 StartZ=0 EndX=1.5 EndY=-5 EndZ=0
    g12: LineSegment StartX=-5.5 StartY=-1.5 StartZ=0 EndX=-5 EndY=-1.5 EndZ=0
    g13: LineSegment StartX=-5 StartY=-1.5 StartZ=0 EndX=-5 EndY=1.5 EndZ=0
    g14: LineSegment StartX=-5 StartY=1.5 StartZ=0 EndX=-5.5 EndY=1.5 EndZ=0
    g15: LineSegment StartX=-5.5 StartY=1.5 StartZ=0 EndX=-5.5 EndY=-1.5 EndZ=0
  constraints (44):
    c: Coincident(g0,g1)
    c: Coincident(g1,g2)
    c: Coincident(g2,g3)
    c: Coincident(g3,g0)
    c: Horizontal(g0)
    c: Vertical(g1)
    c: Vertical(g3)
    c: Coincident(g4,g5)
    c: Coincident(g5,g6)
    c: Coincident(g6,g7)
    c: Coincident(g7,g4)
    c: Horizontal(g4)
    c: Horizontal(g6)
    c: Vertical(g7)
    c: Coincident(g8,g9)
    c: Coincident(g9,g10)
    c: Coincident(g10,g11)
    c: Coincident(g11,g8)
    c: Horizontal(g8)
    c: Horizontal(g10)
    c: Vertical(g9)
    c: Vertical(g11)
    c: Coincident(g12,g13)
    c: Coincident(g13,g14)
    c: Coincident(g14,g15)
    c: Coincident(g15,g12)
    c: Horizontal(g12)
    c: Horizontal(g14)
    c: Vertical(g13)
    c: Vertical(g15)
    c: Symmetric(g13,g6,g-2)
    c: Symmetric(g0,g8,g-1)
    c: Equal(g2,g15)
    c: Equal(g15,g5)
    c: Equal(g5,g10)
    c: Equal(g11,g4)
    c: Equal(g4,g1)
    c: Equal(g1,g14)
    c: DistanceX(g13,g6) = 10
    c: DistanceY(g8,g0) = 10
    c: Symmetric(g1,g2,g-2)
    c: Symmetric(g5,g4,g-1)
    c: DistanceX(g2,g2) = 3
    c: DistanceY(g3,g3) = 0.5
FEATURE [PartDesign::Pad] Pad1171
  BaseFeature = -> Fillet005
  Length = 10
  Length2 = 100
  Placement = pos=(0,0,0) rot=(1,0,0;1.5708rad)
  Profile = -> Sketch2590
  Type = 0
FEATURE [PartDesign::Fillet] Fillet271
  Base = -> Pad1171 [Edge53,Edge50,Edge44,Edge40,Edge66,Edge69,Edge56,Edge60]
  BaseFeature = -> Pad1171
  Placement = pos=(0,0,0) rot=(1,0,0;1.5708rad)
  Radius = 1.4
FEATURE [Sketcher::SketchObject] Sketch2613
  MapMode = 5
  Placement = pos=(5.5,0,0) rot=(0.707107,0,0.707107;3.14159rad)
  Support = -> [Fillet271]
  sketch-geometry (4):
    g0: ArcOfCircle CenterX=-18 CenterY=0 CenterZ=0 NormalX=0 NormalY=0 NormalZ=1 AngleXU=0 Radius=0.5 StartAngle=1.5708 EndAngle=4.71239
    g1: ArcOfCircle CenterX=-16 CenterY=0 CenterZ=0 NormalX=0 NormalY=0 NormalZ=1 AngleXU=0 Radius=0.5 StartAngle=4.71239 EndAngle=7.85398
    g2: LineSegment StartX=-18 StartY=-0.5 StartZ=0 EndX=-16 EndY=-0.5 EndZ=0
    g3: LineSegment StartX=-18 StartY=0.5 StartZ=0 EndX=-16 EndY=0.5 EndZ=0
  constraints (10):
    c: Tangent(g0,g3) = 1.5708
    c: Tangent(g0,g2) = -1.5708
    c: Tangent(g2,g1) = -1.5708
    c: Tangent(g3,g1) = 1.5708
    c: Horizontal(g2)
    c: Equal(g0,g1)
    c: PointOnObject(g0,g-1)
    c: DistanceX(g1,g-1) = 16
    c: DistanceX(g3,g3) = 2
    c: Radius(g0) = 0.5
FEATURE [PartDesign::Pocket] Pocket918
  BaseFeature = -> Fillet271
  Length = 5
  Length2 = 100
  Placement = pos=(0,0,0) rot=(1,0,0;1.5708rad)
  Profile = -> Sketch2613
  Type = 1
FEATURE [Sketcher::SketchObject] Sketch2612
  MapMode = 5
  Placement = pos=(0,-5.5,6.1e-15) rot=(1,0,0;1.5708rad)
  Support = -> [Pocket918]
  sketch-geometry (4):
    g0: ArcOfCircle CenterX=0 CenterY=-18 CenterZ=0 NormalX=0 NormalY=0 NormalZ=1 AngleXU=0 Radius=0.5 StartAngle=3.14159 EndAngle=6.28319
    g1: ArcOfCircle CenterX=-1e-16 CenterY=-16 CenterZ=0 NormalX=0 NormalY=0 NormalZ=1 AngleXU=0 Radius=0.5 StartAngle=-1.8e-15 EndAngle=3.14159
    g2: LineSegment StartX=0.5 StartY=-18 StartZ=0 EndX=0.5 EndY=-16 EndZ=0
    g3: LineSegment StartX=-0.5 StartY=-18 StartZ=0 EndX=-0.5 EndY=-16 EndZ=0
  constraints (10):
    c: Tangent(g0,g3) = 1.5708
    c: Tangent(g0,g2) = -1.5708
    c: Tangent(g2,g1) = -1.5708
    c: Tangent(g3,g1) = 1.5708
    c: Vertical(g2)
    c: Equal(g0,g1)
    c: PointOnObject(g0,g-2)
    c: DistanceY(g1,g-1) = 16
    c: DistanceY(g2,g2) = 2
    c: Radius(g1) = 0.5
FEATURE [PartDesign::Pocket] Pocket919
  BaseFeature = -> Pocket918
  Length = 5
  Length2 = 100
  Placement = pos=(0,0,0) rot=(1,0,0;1.5708rad)
  Profile = -> Sketch2612
  Type = 1
FEATURE [PartDesign::Body] Body789  label="Push Button Case"
  Group = -> [Sketch2611,Revolution058,Fillet005,Sketch2590,Pad1171,Fillet271,Sketch2613,Pocket918,Sketch2612,Pocket919]
  Origin = -> Origin1117
  Tip = -> Pocket919
FEATURE [PartDesign::Fillet] Fillet272
  Base = -> Revolution059 [Edge2,Edge1]
  BaseFeature = -> Revolution059
  Placement = pos=(0,0,0) rot=(1,0,0;1.5708rad)
  Radius = 0.15
FEATURE [PartDesign::Body] Body788  label="Push Button LED"
  Group = -> [Sketch2614,Revolution059,Fillet272]
  Origin = -> Origin1118
  Tip = -> Fillet272
FEATURE [App::Part] Part307  label="Pushbutton"
  Group = -> [Body789,Body788]
  Origin = -> Origin1115
FEATURE [App::Part] Part312  label="Push Button with LED - 19mm"
  Group = -> [Body793,Part307]
  Origin = -> Origin1110
  Placement = pos=(87,40,20) rot=(0,1,0;3.14159rad)
FEATURE [Sketcher::SketchObject] Sketch2620
  MapMode = 5
  Support = -> [XY_Plane1122]
  sketch-geometry (1):
    g0: Circle CenterX=0 CenterY=0 CenterZ=0 NormalX=0 NormalY=0 NormalZ=1 AngleXU=0 Radius=1.9
  constraints (2):
    c: Coincident(g0,g-1)
    c: Radius(g0) = 1.9
FEATURE [PartDesign::Pad] Pad1174  label="M3x8 Head183"
  Length = 2
  Length2 = 100
  Profile = -> Sketch2620
  Type = 0
FEATURE [Sketcher::SketchObject] Sketch2621
  MapMode = 5
  Placement = pos=(0,0,2) rot=(0,0,1;0rad)
  Support = -> [Pad1174]
  sketch-geometry (1):
    g0: Circle CenterX=0 CenterY=0 CenterZ=0 NormalX=0 NormalY=0 NormalZ=1 AngleXU=0 Radius=1
  constraints (2):
    c: Coincident(g0,g-1)
    c: Radius(g0) = 1
FEATURE [PartDesign::Pad] Pad1172  label="M3x8 Thread183"
  BaseFeature = -> Pad1174
  Length = 8
  Length2 = 100
  Profile = -> Sketch2621
  Type = 0
FEATURE [PartDesign::Body] Body795  label="M2x010"
  Group = -> [Sketch2607,Pad1180,Sketch2608,Pad1179,Sketch2606,Pocket920,Chamfer596]
  Origin = -> Origin1120
  Placement = pos=(0,30,0) rot=(0,0,1;0rad)
  Tip = -> Chamfer596
FEATURE [Sketcher::SketchObject] Sketch2623
  MapMode = 5
  Support = -> [XY_Plane1120]
  sketch-geometry (1):
    g0: Circle CenterX=0 CenterY=0 CenterZ=0 NormalX=0 NormalY=0 NormalZ=1 AngleXU=0 Radius=1.9
  constraints (2):
    c: Coincident(g0,g-1)
    c: Radius(g0) = 1.9
FEATURE [PartDesign::Pad] Pad1177  label="M3x8 Head184"
  Length = 2
  Length2 = 100
  Profile = -> Sketch2623
  Type = 0
FEATURE [Sketcher::SketchObject] Sketch2624
  MapMode = 5
  Placement = pos=(0,0,2) rot=(0,0,1;0rad)
  Support = -> [Pad1177]
  sketch-geometry (1):
    g0: Circle CenterX=0 CenterY=0 CenterZ=0 NormalX=0 NormalY=0 NormalZ=1 AngleXU=0 Radius=1
  constraints (2):
    c: Coincident(g0,g-1)
    c: Radius(g0) = 1
FEATURE [PartDesign::Pad] Pad1182  label="M3x8 Thread186"
  BaseFeature = -> Pad1177
  Length = 8
  Length2 = 100
  Profile = -> Sketch2624
  Type = 0
FEATURE [Sketcher::SketchObject] Sketch2625
  MapMode = 5
  Placement = pos=(0,0,0) rot=(1,0,0;3.14159rad)
  Support = -> [Pad1182]
  sketch-geometry (7):
    g0: LineSegment StartX=0.77 StartY=0.44456 StartZ=0 EndX=0 EndY=0.889119 EndZ=0
    g1: LineSegment StartX=0 StartY=0.889119 StartZ=0 EndX=-0.77 EndY=0.44456 EndZ=0
    g2: LineSegment StartX=-0.77 StartY=0.44456 StartZ=0 EndX=-0.77 EndY=-0.44456 EndZ=0
    g3: LineSegment StartX=-0.77 StartY=-0.44456 StartZ=0 EndX=3.85628e-11 EndY=-0.889119 EndZ=0
    g4: LineSegment StartX=3.85628e-11 StartY=-0.889119 StartZ=0 EndX=0.77 EndY=-0.44456 EndZ=0
    g5: LineSegment StartX=0.77 StartY=-0.44456 StartZ=0 EndX=0.77 EndY=0.44456 EndZ=0
    g6: Circle [constr] CenterX=0 CenterY=0 CenterZ=0 NormalX=0 NormalY=0 NormalZ=1 AngleXU=0 Radius=0.889119
  constraints (16):
    c: Coincident(g0,g1)
    c: Coincident(g1,g2)
    c: Coincident(g2,g3)
    c: Coincident(g3,g4)
    c: Coincident(g4,g5)
    c: Coincident(g5,g0)
    c: Equal(g0, g1-g5) x5
    c: PointOnObject(g0,g6)
    c: PointOnObject(g1,g6)
    c: PointOnObject(g2,g6)
    c: PointOnObject(g3,g6)
    c: PointOnObject(g4,g6)
    c: PointOnObject(g5,g6)
    c: Coincident(g6,g-1)
    c: PointOnObject(g0,g-2)
    c: DistanceX(g1,g0) = 1.54
FEATURE [PartDesign::Pocket] Pocket922  label="M3x8 Wrench186"
  BaseFeature = -> Pad1182
  Length = 1
  Length2 = 100
  Profile = -> Sketch2625
  Type = 0
FEATURE [PartDesign::Chamfer] Chamfer600  label="M3x8 Smooth184"
  Base = -> Pocket922 [Face11,Edge2,Edge24,Edge3]
  BaseFeature = -> Pocket922
  Size = 0.2
FEATURE [PartDesign::Body] Body786  label="M2x011"
  Group = -> [Sketch2623,Pad1177,Sketch2624,Pad1182,Sketch2625,Pocket922,Chamfer600]
  Origin = -> Origin1114
  Placement = pos=(50,30,0) rot=(0,0,1;0rad)
  Tip = -> Chamfer600
FEATURE [Sketcher::SketchObject] Sketch2627
  MapMode = 5
  Support = -> [XY_Plane1128]
  sketch-geometry (8):
    g0: LineSegment StartX=0 StartY=2.3094 StartZ=0 EndX=-2 EndY=1.1547 EndZ=0
    g1: LineSegment StartX=-2 StartY=1.1547 StartZ=0 EndX=-2 EndY=-1.1547 EndZ=0
    g2: LineSegment StartX=-2 StartY=-1.1547 StartZ=0 EndX=-2e-16 EndY=-2.3094 EndZ=0
    g3: LineSegment StartX=-2e-16 StartY=-2.3094 StartZ=0 EndX=2 EndY=-1.1547 EndZ=0
    g4: LineSegment StartX=2 StartY=-1.1547 StartZ=0 EndX=2 EndY=1.1547 EndZ=0
    g5: LineSegment StartX=2 StartY=1.1547 StartZ=0 EndX=0 EndY=2.3094 EndZ=0
    g6: Circle [constr] CenterX=0 CenterY=0 CenterZ=0 NormalX=0 NormalY=0 NormalZ=1 AngleXU=0 Radius=2.3094
    g7: Circle CenterX=0 CenterY=0 CenterZ=0 NormalX=0 NormalY=0 NormalZ=1 AngleXU=0 Radius=1
  constraints (18):
    c: Coincident(g0,g1)
    c: Coincident(g1,g2)
    c: Coincident(g2,g3)
    c: Coincident(g3,g4)
    c: Coincident(g4,g5)
    c: Coincident(g5,g0)
    c: Equal(g0, g1-g5) x5
    c: PointOnObject(g0,g6)
    c: PointOnObject(g1,g6)
    c: PointOnObject(g2,g6)
    c: PointOnObject(g3,g6)
    c: PointOnObject(g4,g6)
    c: PointOnObject(g5,g6)
    c: Coincident(g6,g-1)
    c: PointOnObject(g5,g-2)
    c: DistanceX(g0,g4) = 4
    c: Coincident(g7,g-1)
    c: Radius(g7) = 1
FEATURE [PartDesign::Pad] Pad1178  label="M3 Nut Primitive247"
  Length = 0.6
  Length2 = 0.6
  Profile = -> Sketch2627
  Type = 4
FEATURE [Sketcher::SketchObject] Sketch2626
  ExternalGeometry = -> [Pad1178]
  MapMode = 5
  Placement = pos=(0,0,0) rot=(0.57735,0.57735,0.57735;2.0944rad)
  Support = -> [YZ_Plane1120]
  sketch-geometry (6):
    g0: LineSegment StartX=-1.9594 StartY=0.6 StartZ=0 EndX=-2.8094 EndY=0.6 EndZ=0
    g1: LineSegment StartX=-2.8094 StartY=0.6 StartZ=0 EndX=-2.8094 EndY=-0.6 EndZ=0
    g2: LineSegment StartX=-2.8094 StartY=-0.6 StartZ=0 EndX=-1.9594 EndY=-0.6 EndZ=0
    g3: LineSegment StartX=-1.9594 StartY=-0.6 StartZ=0 EndX=-2.3094 EndY=-0.4 EndZ=0
    g4: LineSegment StartX=-2.3094 StartY=-0.4 StartZ=0 EndX=-2.3094 EndY=0.4 EndZ=0
    g5: LineSegment StartX=-2.3094 StartY=0.4 StartZ=0 EndX=-1.9594 EndY=0.6 EndZ=0
  constraints (15):
    c: Horizontal(g0)
    c: Coincident(g0,g1)
    c: Coincident(g1,g2)
    c: Coincident(g2,g3)
    c: Coincident(g3,g4)
    c: Coincident(g4,g5)
    c: Coincident(g5,g0)
    c: Symmetric(g4,g3,g-1)
    c: Symmetric(g0,g2,g-1)
    c: Symmetric(g1,g0,g-1)
    c: DistanceX(g0,g4) = 0.5
    c: DistanceY(g3,g4) = 0.8
    c: DistanceY(g1,g0) = 1.2
    c: PointOnObject(g3,g-3)
    c: DistanceX(g4,g0) = 0.35
FEATURE [PartDesign::Groove] Groove255  label="M3 Nut Smooth246"
  Angle = 360
  Axis = (-2e-16,3e-16,1)
  Base = (0,0,0)
  BaseFeature = -> Pad1178
  Profile = -> Sketch2626
  ReferenceAxis = -> Sketch2626 [V_Axis]
  Reversed = true
FEATURE [PartDesign::Chamfer] Chamfer601  label="M3 Nut Smooth Hole248"
  Base = -> Groove255 [Edge24,Edge23]
  BaseFeature = -> Groove255
  Size = 0.2
FEATURE [Sketcher::SketchObject] Sketch2628
  MapMode = 5
  Support = -> [XY_Plane1128]
FEATURE [Sketcher::SketchObject] Sketch2630
  MapMode = 5
  Support = -> [XY_Plane1128]
FEATURE [PartDesign::Body] Body792  label="M2 Nut"
  Group = -> [Sketch2627,Pad1178,Sketch2626,Groove255,Chamfer601,Sketch2628,Sketch2630]
  Origin = -> Origin1130
  Placement = pos=(14.5,25,0) rot=(0,0,1;0rad)
  Tip = -> Chamfer601
FEATURE [Sketcher::SketchObject] Sketch2632
  MapMode = 5
  Placement = pos=(0,0,0) rot=(1,0,0;3.14159rad)
  Support = -> [Pad1172]
  sketch-geometry (7):
    g0: LineSegment StartX=0.77 StartY=0.44456 StartZ=0 EndX=0 EndY=0.889119 EndZ=0
    g1: LineSegment StartX=0 StartY=0.889119 StartZ=0 EndX=-0.77 EndY=0.44456 EndZ=0
    g2: LineSegment StartX=-0.77 StartY=0.44456 StartZ=0 EndX=-0.77 EndY=-0.44456 EndZ=0
    g3: LineSegment StartX=-0.77 StartY=-0.44456 StartZ=0 EndX=3.85628e-11 EndY=-0.889119 EndZ=0
    g4: LineSegment StartX=3.85628e-11 StartY=-0.889119 StartZ=0 EndX=0.77 EndY=-0.44456 EndZ=0
    g5: LineSegment StartX=0.77 StartY=-0.44456 StartZ=0 EndX=0.77 EndY=0.44456 EndZ=0
    g6: Circle [constr] CenterX=0 CenterY=0 CenterZ=0 NormalX=0 NormalY=0 NormalZ=1 AngleXU=0 Radius=0.889119
  constraints (16):
    c: Coincident(g0,g1)
    c: Coincident(g1,g2)
    c: Coincident(g2,g3)
    c: Coincident(g3,g4)
    c: Coincident(g4,g5)
    c: Coincident(g5,g0)
    c: Equal(g0, g1-g5) x5
    c: PointOnObject(g0,g6)
    c: PointOnObject(g1,g6)
    c: PointOnObject(g2,g6)
    c: PointOnObject(g3,g6)
    c: PointOnObject(g4,g6)
    c: PointOnObject(g5,g6)
    c: Coincident(g6,g-1)
    c: PointOnObject(g0,g-2)
    c: DistanceX(g1,g0) = 1.54
FEATURE [PartDesign::Pocket] Pocket917  label="M3x8 Wrench183"
  BaseFeature = -> Pad1172
  Length = 1
  Length2 = 100
  Profile = -> Sketch2632
  Type = 0
FEATURE [PartDesign::Chamfer] Chamfer599  label="M3x8 Smooth183"
  Base = -> Pocket917 [Face11,Edge2,Edge24,Edge3]
  BaseFeature = -> Pocket917
  Size = 0.2
FEATURE [PartDesign::Body] Body787  label="M2x8"
  Group = -> [Sketch2620,Pad1174,Sketch2621,Pad1172,Sketch2632,Pocket917,Chamfer599]
  Origin = -> Origin1122
  Tip = -> Chamfer599
FEATURE [Sketcher::SketchObject] Sketch2633
  MapMode = 5
  Support = -> [XY_Plane1125]
  sketch-geometry (1):
    g0: Circle CenterX=0 CenterY=0 CenterZ=0 NormalX=0 NormalY=0 NormalZ=1 AngleXU=0 Radius=1.9
  constraints (2):
    c: Coincident(g0,g-1)
    c: Radius(g0) = 1.9
FEATURE [PartDesign::Pad] Pad1181  label="M3x8 Head186"
  Length = 2
  Length2 = 100
  Profile = -> Sketch2633
  Type = 0
FEATURE [Sketcher::SketchObject] Sketch2629
  MapMode = 5
  Placement = pos=(0,0,2) rot=(0,0,1;0rad)
  Support = -> [Pad1181]
  sketch-geometry (1):
    g0: Circle CenterX=0 CenterY=0 CenterZ=0 NormalX=0 NormalY=0 NormalZ=1 AngleXU=0 Radius=1
  constraints (2):
    c: Coincident(g0,g-1)
    c: Radius(g0) = 1
FEATURE [PartDesign::Pad] Pad1173  label="M3x8 Thread184"
  BaseFeature = -> Pad1181
  Length = 8
  Length2 = 100
  Profile = -> Sketch2629
  Type = 0
FEATURE [Sketcher::SketchObject] Sketch2622
  MapMode = 5
  Placement = pos=(0,0,0) rot=(1,0,0;3.14159rad)
  Support = -> [Pad1173]
  sketch-geometry (7):
    g0: LineSegment StartX=0.77 StartY=0.44456 StartZ=0 EndX=0 EndY=0.889119 EndZ=0
    g1: LineSegment StartX=0 StartY=0.889119 StartZ=0 EndX=-0.77 EndY=0.44456 EndZ=0
    g2: LineSegment StartX=-0.77 StartY=0.44456 StartZ=0 EndX=-0.77 EndY=-0.44456 EndZ=0
    g3: LineSegment StartX=-0.77 StartY=-0.44456 StartZ=0 EndX=3.85628e-11 EndY=-0.889119 EndZ=0
    g4: LineSegment StartX=3.85628e-11 StartY=-0.889119 StartZ=0 EndX=0.77 EndY=-0.44456 EndZ=0
    g5: LineSegment StartX=0.77 StartY=-0.44456 StartZ=0 EndX=0.77 EndY=0.44456 EndZ=0
    g6: Circle [constr] CenterX=0 CenterY=0 CenterZ=0 NormalX=0 NormalY=0 NormalZ=1 AngleXU=0 Radius=0.889119
  constraints (16):
    c: Coincident(g0,g1)
    c: Coincident(g1,g2)
    c: Coincident(g2,g3)
    c: Coincident(g3,g4)
    c: Coincident(g4,g5)
    c: Coincident(g5,g0)
    c: Equal(g0, g1-g5) x5
    c: PointOnObject(g0,g6)
    c: PointOnObject(g1,g6)
    c: PointOnObject(g2,g6)
    c: PointOnObject(g3,g6)
    c: PointOnObject(g4,g6)
    c: PointOnObject(g5,g6)
    c: Coincident(g6,g-1)
    c: PointOnObject(g0,g-2)
    c: DistanceX(g1,g0) = 1.54
FEATURE [PartDesign::Pocket] Pocket921  label="M3x8 Wrench185"
  BaseFeature = -> Pad1173
  Length = 1
  Length2 = 100
  Profile = -> Sketch2622
  Type = 0
FEATURE [PartDesign::Chamfer] Chamfer602  label="M3x8 Smooth185"
  Base = -> Pocket921 [Face11,Edge2,Edge24,Edge3]
  BaseFeature = -> Pocket921
  Size = 0.2
FEATURE [PartDesign::Body] Body794  label="M2x009"
  Group = -> [Sketch2633,Pad1181,Sketch2629,Pad1173,Sketch2622,Pocket921,Chamfer602]
  Origin = -> Origin1126
  Placement = pos=(50,0,0) rot=(0,0,1;0rad)
  Tip = -> Chamfer602
FEATURE [App::Part] Part314  label="TFT Screws"
  Group = -> [Body787,Body794,Body795,Body786]
  Origin = -> Origin1112
  Placement = pos=(14.5,25,-2) rot=(0,0,1;0rad)
FEATURE [Sketcher::SketchObject] Sketch2634
  MapMode = 5
  Support = -> [XY_Plane1129]
FEATURE [Sketcher::SketchObject] Sketch2635
  MapMode = 5
  Support = -> [XY_Plane1129]
FEATURE [Sketcher::SketchObject] Sketch233
  MapMode = 5
  Support = -> [XY_Plane1117]
  sketch-geometry (8):
    g0: LineSegment StartX=0 StartY=2.3094 StartZ=0 EndX=-2 EndY=1.1547 EndZ=0
    g1: LineSegment StartX=-2 StartY=1.1547 StartZ=0 EndX=-2 EndY=-1.1547 EndZ=0
    g2: LineSegment StartX=-2 StartY=-1.1547 StartZ=0 EndX=-2e-16 EndY=-2.3094 EndZ=0
    g3: LineSegment StartX=-2e-16 StartY=-2.3094 StartZ=0 EndX=2 EndY=-1.1547 EndZ=0
    g4: LineSegment StartX=2 StartY=-1.1547 StartZ=0 EndX=2 EndY=1.1547 EndZ=0
    g5: LineSegment StartX=2 StartY=1.1547 StartZ=0 EndX=0 EndY=2.3094 EndZ=0
    g6: Circle [constr] CenterX=0 CenterY=0 CenterZ=0 NormalX=0 NormalY=0 NormalZ=1 AngleXU=0 Radius=2.3094
    g7: Circle CenterX=0 CenterY=0 CenterZ=0 NormalX=0 NormalY=0 NormalZ=1 AngleXU=0 Radius=1
  constraints (18):
    c: Coincident(g0,g1)
    c: Coincident(g1,g2)
    c: Coincident(g2,g3)
    c: Coincident(g3,g4)
    c: Coincident(g4,g5)
    c: Coincident(g5,g0)
    c: Equal(g0, g1-g5) x5
    c: PointOnObject(g0,g6)
    c: PointOnObject(g1,g6)
    c: PointOnObject(g2,g6)
    c: PointOnObject(g3,g6)
    c: PointOnObject(g4,g6)
    c: PointOnObject(g5,g6)
    c: Coincident(g6,g-1)
    c: PointOnObject(g5,g-2)
    c: DistanceX(g0,g4) = 4
    c: Coincident(g7,g-1)
    c: Radius(g7) = 1
FEATURE [PartDesign::Pad] Pad1183  label="M3 Nut Primitive248"
  Length = 0.6
  Length2 = 0.6
  Profile = -> Sketch233
  Type = 4
FEATURE [Sketcher::SketchObject] Sketch2636
  ExternalGeometry = -> [Pad1183]
  MapMode = 5
  Placement = pos=(0,0,0) rot=(0.57735,0.57735,0.57735;2.0944rad)
  Support = -> [YZ_Plane1111]
  sketch-geometry (6):
    g0: LineSegment StartX=-1.9594 StartY=0.6 StartZ=0 EndX=-2.8094 EndY=0.6 EndZ=0
    g1: LineSegment StartX=-2.8094 StartY=0.6 StartZ=0 EndX=-2.8094 EndY=-0.6 EndZ=0
    g2: LineSegment StartX=-2.8094 StartY=-0.6 StartZ=0 EndX=-1.9594 EndY=-0.6 EndZ=0
    g3: LineSegment StartX=-1.9594 StartY=-0.6 StartZ=0 EndX=-2.3094 EndY=-0.4 EndZ=0
    g4: LineSegment StartX=-2.3094 StartY=-0.4 StartZ=0 EndX=-2.3094 EndY=0.4 EndZ=0
    g5: LineSegment StartX=-2.3094 StartY=0.4 StartZ=0 EndX=-1.9594 EndY=0.6 EndZ=0
  constraints (15):
    c: Horizontal(g0)
    c: Coincident(g0,g1)
    c: Coincident(g1,g2)
    c: Coincident(g2,g3)
    c: Coincident(g3,g4)
    c: Coincident(g4,g5)
    c: Coincident(g5,g0)
    c: Symmetric(g4,g3,g-1)
    c: Symmetric(g0,g2,g-1)
    c: Symmetric(g1,g0,g-1)
    c: DistanceX(g0,g4) = 0.5
    c: DistanceY(g3,g4) = 0.8
    c: DistanceY(g1,g0) = 1.2
    c: PointOnObject(g3,g-3)
    c: DistanceX(g4,g0) = 0.35
FEATURE [PartDesign::Groove] Groove257  label="M3 Nut Smooth248"
  Angle = 360
  Axis = (-2e-16,3e-16,1)
  Base = (0,0,0)
  BaseFeature = -> Pad1183
  Profile = -> Sketch2636
  ReferenceAxis = -> Sketch2636 [V_Axis]
  Reversed = true
FEATURE [PartDesign::Chamfer] Chamfer598  label="M3 Nut Smooth Hole247"
  Base = -> Groove257 [Edge24,Edge23]
  BaseFeature = -> Groove257
  Size = 0.2
FEATURE [Sketcher::SketchObject] Sketch2637
  MapMode = 5
  Support = -> [XY_Plane1117]
FEATURE [Sketcher::SketchObject] Sketch2638
  MapMode = 5
  Support = -> [XY_Plane1129]
  sketch-geometry (8):
    g0: LineSegment StartX=0 StartY=2.3094 StartZ=0 EndX=-2 EndY=1.1547 EndZ=0
    g1: LineSegment StartX=-2 StartY=1.1547 StartZ=0 EndX=-2 EndY=-1.1547 EndZ=0
    g2: LineSegment StartX=-2 StartY=-1.1547 StartZ=0 EndX=-2e-16 EndY=-2.3094 EndZ=0
    g3: LineSegment StartX=-2e-16 StartY=-2.3094 StartZ=0 EndX=2 EndY=-1.1547 EndZ=0
    g4: LineSegment StartX=2 StartY=-1.1547 StartZ=0 EndX=2 EndY=1.1547 EndZ=0
    g5: LineSegment StartX=2 StartY=1.1547 StartZ=0 EndX=0 EndY=2.3094 EndZ=0
    g6: Circle [constr] CenterX=0 CenterY=0 CenterZ=0 NormalX=0 NormalY=0 NormalZ=1 AngleXU=0 Radius=2.3094
    g7: Circle CenterX=0 CenterY=0 CenterZ=0 NormalX=0 NormalY=0 NormalZ=1 AngleXU=0 Radius=1
  constraints (18):
    c: Coincident(g0,g1)
    c: Coincident(g1,g2)
    c: Coincident(g2,g3)
    c: Coincident(g3,g4)
    c: Coincident(g4,g5)
    c: Coincident(g5,g0)
    c: Equal(g0, g1-g5) x5
    c: PointOnObject(g0,g6)
    c: PointOnObject(g1,g6)
    c: PointOnObject(g2,g6)
    c: PointOnObject(g3,g6)
    c: PointOnObject(g4,g6)
    c: PointOnObject(g5,g6)
    c: Coincident(g6,g-1)
    c: PointOnObject(g5,g-2)
    c: DistanceX(g0,g4) = 4
    c: Coincident(g7,g-1)
    c: Radius(g7) = 1
FEATURE [PartDesign::Pad] Pad1175  label="M3 Nut Primitive245"
  Length = 0.6
  Length2 = 0.6
  Profile = -> Sketch2638
  Type = 4
FEATURE [Sketcher::SketchObject] Sketch2631
  ExternalGeometry = -> [Pad1175]
  MapMode = 5
  Placement = pos=(0,0,0) rot=(0.57735,0.57735,0.57735;2.0944rad)
  Support = -> [YZ_Plane1123]
  sketch-geometry (6):
    g0: LineSegment StartX=-1.9594 StartY=0.6 StartZ=0 EndX=-2.8094 EndY=0.6 EndZ=0
    g1: LineSegment StartX=-2.8094 StartY=0.6 StartZ=0 EndX=-2.8094 EndY=-0.6 EndZ=0
    g2: LineSegment StartX=-2.8094 StartY=-0.6 StartZ=0 EndX=-1.9594 EndY=-0.6 EndZ=0
    g3: LineSegment StartX=-1.9594 StartY=-0.6 StartZ=0 EndX=-2.3094 EndY=-0.4 EndZ=0
    g4: LineSegment StartX=-2.3094 StartY=-0.4 StartZ=0 EndX=-2.3094 EndY=0.4 EndZ=0
    g5: LineSegment StartX=-2.3094 StartY=0.4 StartZ=0 EndX=-1.9594 EndY=0.6 EndZ=0
  constraints (15):
    c: Horizontal(g0)
    c: Coincident(g0,g1)
    c: Coincident(g1,g2)
    c: Coincident(g2,g3)
    c: Coincident(g3,g4)
    c: Coincident(g4,g5)
    c: Coincident(g5,g0)
    c: Symmetric(g4,g3,g-1)
    c: Symmetric(g0,g2,g-1)
    c: Symmetric(g1,g0,g-1)
    c: DistanceX(g0,g4) = 0.5
    c: DistanceY(g3,g4) = 0.8
    c: DistanceY(g1,g0) = 1.2
    c: PointOnObject(g3,g-3)
    c: DistanceX(g4,g0) = 0.35
FEATURE [PartDesign::Groove] Groove256  label="M3 Nut Smooth247"
  Angle = 360
  Axis = (-2e-16,3e-16,1)
  Base = (0,0,0)
  BaseFeature = -> Pad1175
  Profile = -> Sketch2631
  ReferenceAxis = -> Sketch2631 [V_Axis]
  Reversed = true
FEATURE [PartDesign::Chamfer] Chamfer597  label="M3 Nut Smooth Hole246"
  Base = -> Groove256 [Edge24,Edge23]
  BaseFeature = -> Groove256
  Size = 0.2
FEATURE [PartDesign::Body] Body791  label="M2 Nut001"
  Group = -> [Sketch2638,Pad1175,Sketch2631,Groove256,Chamfer597,Sketch2634,Sketch2635]
  Origin = -> Origin1121
  Placement = pos=(64.5,25,0) rot=(0,0,1;0rad)
  Tip = -> Chamfer597
FEATURE [Sketcher::SketchObject] Sketch2639
  MapMode = 5
  Support = -> [XY_Plane1117]
FEATURE [PartDesign::Body] Body790  label="M2 Nut002"
  Group = -> [Sketch233,Pad1183,Sketch2636,Groove257,Chamfer598,Sketch2637,Sketch2639]
  Origin = -> Origin1131
  Placement = pos=(14.5,55,0) rot=(0,0,1;0rad)
  Tip = -> Chamfer598
FEATURE [App::Part] Part311  label="TFT Nuts"
  Group = -> [Body792,Body791,Body790,Body784]
  Origin = -> Origin1124
  Placement = pos=(0,0,7.25) rot=(0,0,1;0rad)
FEATURE [App::Part] Part313  label="TFT Screws and Nuts"
  Group = -> [Part314,Part311]
  Origin = -> Origin1113
FEATURE [App::Part] Part308  label="Rear Cover Assembly"
  Group = -> [Body785,Part309,Part312,Part313]
  Origin = -> Origin1108
  Placement = pos=(-280.5,-42.5,238.5) rot=(0.57735,-0.57735,0.57735;4.18879rad)
FEATURE [Sketcher::SketchObject] Sketch2641
  MapMode = 5
  Support = -> [XY_Plane1130]
  sketch-geometry (1):
    g0: Circle CenterX=0 CenterY=0 CenterZ=0 NormalX=0 NormalY=0 NormalZ=1 AngleXU=0 Radius=2.75
  constraints (2):
    c: Coincident(g0,g-1)
    c: Radius(g0) = 2.75
FEATURE [Sketcher::SketchObject] Sketch2643
  MapMode = 5
  Support = -> [XY_Plane1132]
  sketch-geometry (1):
    g0: Circle CenterX=0 CenterY=0 CenterZ=0 NormalX=0 NormalY=0 NormalZ=1 AngleXU=0 Radius=2.75
  constraints (2):
    c: Coincident(g0,g-1)
    c: Radius(g0) = 2.75
FEATURE [Sketcher::SketchObject] Sketch2647
  MapMode = 5
  Support = -> [XY_Plane1131]
  sketch-geometry (1):
    g0: Circle CenterX=0 CenterY=0 CenterZ=0 NormalX=0 NormalY=0 NormalZ=1 AngleXU=0 Radius=2.75
  constraints (2):
    c: Coincident(g0,g-1)
    c: Radius(g0) = 2.75
FEATURE [Sketcher::SketchObject] Sketch2651
  MapMode = 5
  Support = -> [XY_Plane1134]
  sketch-geometry (1):
    g0: Circle CenterX=0 CenterY=0 CenterZ=0 NormalX=0 NormalY=0 NormalZ=1 AngleXU=0 Radius=2.75
  constraints (2):
    c: Coincident(g0,g-1)
    c: Radius(g0) = 2.75
FEATURE [PartDesign::Pad] Pad1185  label="M3x8 Head187"
  Length = 3
  Length2 = 100
  Profile = -> Sketch2643
  Type = 0
FEATURE [Sketcher::SketchObject] Sketch2642
  MapMode = 5
  Placement = pos=(0,0,3) rot=(0,0,1;0rad)
  Support = -> [Pad1185]
  sketch-geometry (1):
    g0: Circle CenterX=0 CenterY=0 CenterZ=0 NormalX=0 NormalY=0 NormalZ=1 AngleXU=0 Radius=1.5
  constraints (2):
    c: Coincident(g0,g-1)
    c: Radius(g0) = 1.5
FEATURE [PartDesign::Pad] Pad1188  label="M3x8 Thread190"
  BaseFeature = -> Pad1185
  Length = 8
  Length2 = 100
  Profile = -> Sketch2642
  Type = 0
FEATURE [Sketcher::SketchObject] Sketch2648
  MapMode = 5
  Placement = pos=(0,0,0) rot=(1,0,0;3.14159rad)
  Support = -> [Pad1188]
  sketch-geometry (7):
    g0: LineSegment StartX=1.275 StartY=0.736122 StartZ=0 EndX=0 EndY=1.47224 EndZ=0
    g1: LineSegment StartX=0 StartY=1.47224 StartZ=0 EndX=-1.275 EndY=0.736122 EndZ=0
    g2: LineSegment StartX=-1.275 StartY=0.736122 StartZ=0 EndX=-1.275 EndY=-0.736122 EndZ=0
    g3: LineSegment StartX=-1.275 StartY=-0.736122 StartZ=0 EndX=1.34766e-11 EndY=-1.47224 EndZ=0
    g4: LineSegment StartX=1.34766e-11 StartY=-1.47224 StartZ=0 EndX=1.275 EndY=-0.736122 EndZ=0
    g5: LineSegment StartX=1.275 StartY=-0.736122 StartZ=0 EndX=1.275 EndY=0.736122 EndZ=0
    g6: Circle [constr] CenterX=0 CenterY=0 CenterZ=0 NormalX=0 NormalY=0 NormalZ=1 AngleXU=0 Radius=1.47224
  constraints (16):
    c: Coincident(g0,g1)
    c: Coincident(g1,g2)
    c: Coincident(g2,g3)
    c: Coincident(g3,g4)
    c: Coincident(g4,g5)
    c: Coincident(g5,g0)
    c: Equal(g0, g1-g5) x5
    c: PointOnObject(g0,g6)
    c: PointOnObject(g1,g6)
    c: PointOnObject(g2,g6)
    c: PointOnObject(g3,g6)
    c: PointOnObject(g4,g6)
    c: PointOnObject(g5,g6)
    c: Coincident(g6,g-1)
    c: PointOnObject(g0,g-2)
    c: DistanceX(g1,g0) = 2.55
FEATURE [PartDesign::Pocket] Pocket923  label="M3x8 Wrench187"
  BaseFeature = -> Pad1188
  Length = 1.3
  Length2 = 100
  Profile = -> Sketch2648
  Type = 0
FEATURE [PartDesign::Chamfer] Chamfer603  label="M3x8 Smooth186"
  Base = -> Pocket923 [Face11,Edge2,Edge24,Edge3]
  BaseFeature = -> Pocket923
  Size = 0.2
FEATURE [PartDesign::Body] Body797  label="M3x156"
  Group = -> [Sketch2643,Pad1185,Sketch2642,Pad1188,Sketch2648,Pocket923,Chamfer603]
  Origin = -> Origin1136
  Placement = pos=(-9e-15,-10,76.2) rot=(0,1,0;3.14159rad)
  Tip = -> Chamfer603
FEATURE [PartDesign::Pad] Pad1189  label="M3x8 Head188"
  Length = 3
  Length2 = 100
  Profile = -> Sketch2647
  Type = 0
FEATURE [Sketcher::SketchObject] Sketch2644
  MapMode = 5
  Placement = pos=(0,0,3) rot=(0,0,1;0rad)
  Support = -> [Pad1189]
  sketch-geometry (1):
    g0: Circle CenterX=0 CenterY=0 CenterZ=0 NormalX=0 NormalY=0 NormalZ=1 AngleXU=0 Radius=1.5
  constraints (2):
    c: Coincident(g0,g-1)
    c: Radius(g0) = 1.5
FEATURE [PartDesign::Pad] Pad1186  label="M3x8 Thread188"
  BaseFeature = -> Pad1189
  Length = 8
  Length2 = 100
  Profile = -> Sketch2644
  Type = 0
FEATURE [Sketcher::SketchObject] Sketch2646
  MapMode = 5
  Placement = pos=(0,0,0) rot=(1,0,0;3.14159rad)
  Support = -> [Pad1186]
  sketch-geometry (7):
    g0: LineSegment StartX=1.275 StartY=0.736122 StartZ=0 EndX=0 EndY=1.47224 EndZ=0
    g1: LineSegment StartX=0 StartY=1.47224 StartZ=0 EndX=-1.275 EndY=0.736122 EndZ=0
    g2: LineSegment StartX=-1.275 StartY=0.736122 StartZ=0 EndX=-1.275 EndY=-0.736122 EndZ=0
    g3: LineSegment StartX=-1.275 StartY=-0.736122 StartZ=0 EndX=1.34766e-11 EndY=-1.47224 EndZ=0
    g4: LineSegment StartX=1.34766e-11 StartY=-1.47224 StartZ=0 EndX=1.275 EndY=-0.736122 EndZ=0
    g5: LineSegment StartX=1.275 StartY=-0.736122 StartZ=0 EndX=1.275 EndY=0.736122 EndZ=0
    g6: Circle [constr] CenterX=0 CenterY=0 CenterZ=0 NormalX=0 NormalY=0 NormalZ=1 AngleXU=0 Radius=1.47224
  constraints (16):
    c: Coincident(g0,g1)
    c: Coincident(g1,g2)
    c: Coincident(g2,g3)
    c: Coincident(g3,g4)
    c: Coincident(g4,g5)
    c: Coincident(g5,g0)
    c: Equal(g0, g1-g5) x5
    c: PointOnObject(g0,g6)
    c: PointOnObject(g1,g6)
    c: PointOnObject(g2,g6)
    c: PointOnObject(g3,g6)
    c: PointOnObject(g4,g6)
    c: PointOnObject(g5,g6)
    c: Coincident(g6,g-1)
    c: PointOnObject(g0,g-2)
    c: DistanceX(g1,g0) = 2.55
FEATURE [PartDesign::Pocket] Pocket925  label="M3x8 Wrench189"
  BaseFeature = -> Pad1186
  Length = 1.3
  Length2 = 100
  Profile = -> Sketch2646
  Type = 0
FEATURE [PartDesign::Chamfer] Chamfer606  label="M3x8 Smooth189"
  Base = -> Pocket925 [Face11,Edge2,Edge24,Edge3]
  BaseFeature = -> Pocket925
  Size = 0.2
FEATURE [PartDesign::Body] Body798  label="M3x157"
  Group = -> [Sketch2647,Pad1189,Sketch2644,Pad1186,Sketch2646,Pocket925,Chamfer606]
  Origin = -> Origin1134
  Placement = pos=(0,10,-4.25) rot=(0,0,1;0rad)
  Tip = -> Chamfer606
FEATURE [PartDesign::Pad] Pad1190  label="M3x8 Head189"
  Length = 3
  Length2 = 100
  Profile = -> Sketch2641
  Type = 0
FEATURE [Sketcher::SketchObject] Sketch2645
  MapMode = 5
  Placement = pos=(0,0,3) rot=(0,0,1;0rad)
  Support = -> [Pad1190]
  sketch-geometry (1):
    g0: Circle CenterX=0 CenterY=0 CenterZ=0 NormalX=0 NormalY=0 NormalZ=1 AngleXU=0 Radius=1.5
  constraints (2):
    c: Coincident(g0,g-1)
    c: Radius(g0) = 1.5
FEATURE [PartDesign::Pad] Pad1187  label="M3x8 Thread189"
  BaseFeature = -> Pad1190
  Length = 8
  Length2 = 100
  Profile = -> Sketch2645
  Type = 0
FEATURE [Sketcher::SketchObject] Sketch2640
  MapMode = 5
  Placement = pos=(0,0,0) rot=(1,0,0;3.14159rad)
  Support = -> [Pad1187]
  sketch-geometry (7):
    g0: LineSegment StartX=1.275 StartY=0.736122 StartZ=0 EndX=0 EndY=1.47224 EndZ=0
    g1: LineSegment StartX=0 StartY=1.47224 StartZ=0 EndX=-1.275 EndY=0.736122 EndZ=0
    g2: LineSegment StartX=-1.275 StartY=0.736122 StartZ=0 EndX=-1.275 EndY=-0.736122 EndZ=0
    g3: LineSegment StartX=-1.275 StartY=-0.736122 StartZ=0 EndX=1.34766e-11 EndY=-1.47224 EndZ=0
    g4: LineSegment StartX=1.34766e-11 StartY=-1.47224 StartZ=0 EndX=1.275 EndY=-0.736122 EndZ=0
    g5: LineSegment StartX=1.275 StartY=-0.736122 StartZ=0 EndX=1.275 EndY=0.736122 EndZ=0
    g6: Circle [constr] CenterX=0 CenterY=0 CenterZ=0 NormalX=0 NormalY=0 NormalZ=1 AngleXU=0 Radius=1.47224
  constraints (16):
    c: Coincident(g0,g1)
    c: Coincident(g1,g2)
    c: Coincident(g2,g3)
    c: Coincident(g3,g4)
    c: Coincident(g4,g5)
    c: Coincident(g5,g0)
    c: Equal(g0, g1-g5) x5
    c: PointOnObject(g0,g6)
    c: PointOnObject(g1,g6)
    c: PointOnObject(g2,g6)
    c: PointOnObject(g3,g6)
    c: PointOnObject(g4,g6)
    c: PointOnObject(g5,g6)
    c: Coincident(g6,g-1)
    c: PointOnObject(g0,g-2)
    c: DistanceX(g1,g0) = 2.55
FEATURE [PartDesign::Pocket] Pocket924  label="M3x8 Wrench188"
  BaseFeature = -> Pad1187
  Length = 1.3
  Length2 = 100
  Profile = -> Sketch2640
  Type = 0
FEATURE [PartDesign::Chamfer] Chamfer604  label="M3x8 Smooth187"
  Base = -> Pocket924 [Face11,Edge2,Edge24,Edge3]
  BaseFeature = -> Pocket924
  Size = 0.2
FEATURE [PartDesign::Body] Body796  label="M3x155"
  Group = -> [Sketch2641,Pad1190,Sketch2645,Pad1187,Sketch2640,Pocket924,Chamfer604]
  Origin = -> Origin1132
  Placement = pos=(0,0,-4.25) rot=(0,0,1;0rad)
  Tip = -> Chamfer604
FEATURE [PartDesign::Pad] Pad1191  label="M3x8 Head190"
  Length = 3
  Length2 = 100
  Profile = -> Sketch2651
  Type = 0
FEATURE [Sketcher::SketchObject] Sketch2649
  MapMode = 5
  Placement = pos=(0,0,3) rot=(0,0,1;0rad)
  Support = -> [Pad1191]
  sketch-geometry (1):
    g0: Circle CenterX=0 CenterY=0 CenterZ=0 NormalX=0 NormalY=0 NormalZ=1 AngleXU=0 Radius=1.5
  constraints (2):
    c: Coincident(g0,g-1)
    c: Radius(g0) = 1.5
FEATURE [PartDesign::Pad] Pad1184  label="M3x8 Thread187"
  BaseFeature = -> Pad1191
  Length = 8
  Length2 = 100
  Profile = -> Sketch2649
  Type = 0
FEATURE [Sketcher::SketchObject] Sketch2650
  MapMode = 5
  Placement = pos=(0,0,0) rot=(1,0,0;3.14159rad)
  Support = -> [Pad1184]
  sketch-geometry (7):
    g0: LineSegment StartX=1.275 StartY=0.736122 StartZ=0 EndX=0 EndY=1.47224 EndZ=0
    g1: LineSegment StartX=0 StartY=1.47224 StartZ=0 EndX=-1.275 EndY=0.736122 EndZ=0
    g2: LineSegment StartX=-1.275 StartY=0.736122 StartZ=0 EndX=-1.275 EndY=-0.736122 EndZ=0
    g3: LineSegment StartX=-1.275 StartY=-0.736122 StartZ=0 EndX=1.34766e-11 EndY=-1.47224 EndZ=0
    g4: LineSegment StartX=1.34766e-11 StartY=-1.47224 StartZ=0 EndX=1.275 EndY=-0.736122 EndZ=0
    g5: LineSegment StartX=1.275 StartY=-0.736122 StartZ=0 EndX=1.275 EndY=0.736122 EndZ=0
    g6: Circle [constr] CenterX=0 CenterY=0 CenterZ=0 NormalX=0 NormalY=0 NormalZ=1 AngleXU=0 Radius=1.47224
  constraints (16):
    c: Coincident(g0,g1)
    c: Coincident(g1,g2)
    c: Coincident(g2,g3)
    c: Coincident(g3,g4)
    c: Coincident(g4,g5)
    c: Coincident(g5,g0)
    c: Equal(g0, g1-g5) x5
    c: PointOnObject(g0,g6)
    c: PointOnObject(g1,g6)
    c: PointOnObject(g2,g6)
    c: PointOnObject(g3,g6)
    c: PointOnObject(g4,g6)
    c: PointOnObject(g5,g6)
    c: Coincident(g6,g-1)
    c: PointOnObject(g0,g-2)
    c: DistanceX(g1,g0) = 2.55
FEATURE [PartDesign::Pocket] Pocket926  label="M3x8 Wrench190"
  BaseFeature = -> Pad1184
  Length = 1.3
  Length2 = 100
  Profile = -> Sketch2650
  Type = 0
FEATURE [PartDesign::Chamfer] Chamfer605  label="M3x8 Smooth188"
  Base = -> Pocket926 [Face11,Edge2,Edge24,Edge3]
  BaseFeature = -> Pocket926
  Size = 0.2
FEATURE [PartDesign::Body] Body799  label="M3x158"
  Group = -> [Sketch2651,Pad1191,Sketch2649,Pad1184,Sketch2650,Pocket926,Chamfer605]
  Origin = -> Origin1135
  Placement = pos=(-9e-15,20.05,76.2) rot=(0,1,0;3.14159rad)
  Tip = -> Chamfer605
FEATURE [App::Part] Part315  label="Rear_Cover_Screws001"
  Group = -> [Body796,Body798,Body797,Body799]
  Origin = -> Origin1133
  Placement = pos=(-216.75,-104.5,165.6) rot=(0,0,1;0rad)
FEATURE [Sketcher::SketchObject] Sketch2652
  MapMode = 5
  Placement = pos=(0,0,0) rot=(1,0,0;1.5708rad)
  Support = -> [XZ_Plane1138]
  sketch-geometry (6):
    g0: LineSegment StartX=20 StartY=40 StartZ=0 EndX=90 EndY=40 EndZ=0
    g1: LineSegment StartX=110 StartY=20 StartZ=0 EndX=110 EndY=0 EndZ=0
    g2: LineSegment StartX=110 StartY=0 StartZ=0 EndX=0 EndY=0 EndZ=0
    g3: LineSegment StartX=0 StartY=0 StartZ=0 EndX=0 EndY=20 EndZ=0
    g4: ArcOfCircle CenterX=20 CenterY=20 CenterZ=0 NormalX=0 NormalY=0 NormalZ=1 AngleXU=0 Radius=20 StartAngle=1.5708 EndAngle=3.14159
    g5: ArcOfCircle CenterX=90 CenterY=20 CenterZ=0 NormalX=0 NormalY=0 NormalZ=1 AngleXU=0 Radius=20 StartAngle=0 EndAngle=1.5708
  constraints (15):
    c: Coincident(g1,g2)
    c: Coincident(g2,g3)
    c: Horizontal(g0)
    c: Horizontal(g2)
    c: Vertical(g1)
    c: Vertical(g3)
    c: Tangent(g3,g4) = 1.5708
    c: Tangent(g0,g4) = 1.5708
    c: Tangent(g0,g5) = 1.5708
    c: Tangent(g1,g5) = 1.5708
    c: DistanceX(g2,g2) = 110
    c: Equal(g5,g4)
    c: Radius(g4) = 20
    c: Coincident(g2,g-1)
    c: DistanceY(g2,g0) = 40
FEATURE [Sketcher::SketchObject] Sketch2656
  AttachmentOffset = pos=(0,0,-108.85) rot=(0,0,1;0rad)
  MapMode = 5
  Placement = pos=(0,108.85,2.42e-14) rot=(1,0,0;1.5708rad)
  Support = -> [XZ_Plane1138]
  sketch-geometry (14):
    g0: LineSegment StartX=0 StartY=20 StartZ=0 EndX=6.5 EndY=20 EndZ=0
    g1: LineSegment StartX=6.5 StartY=20 StartZ=0 EndX=6.5 EndY=34.7564 EndZ=0
    g2: LineSegment StartX=36.75 StartY=40 StartZ=0 EndX=36.75 EndY=33.5 EndZ=0
    g3: LineSegment StartX=36.75 StartY=33.5 StartZ=0 EndX=43.25 EndY=33.5 EndZ=0
    g4: LineSegment StartX=43.25 StartY=33.5 StartZ=0 EndX=43.25 EndY=40 EndZ=0
    g5: LineSegment StartX=43.25 StartY=40 StartZ=0 EndX=36.75 EndY=40 EndZ=0
    g6: LineSegment StartX=66.75 StartY=40 StartZ=0 EndX=66.75 EndY=33.5 EndZ=0
    g7: LineSegment StartX=66.75 StartY=33.5 StartZ=0 EndX=73.25 EndY=33.5 EndZ=0
    g8: LineSegment StartX=73.25 StartY=33.5 StartZ=0 EndX=73.25 EndY=40 EndZ=0
    g9: LineSegment StartX=73.25 StartY=40 StartZ=0 EndX=66.75 EndY=40 EndZ=0
    g10: LineSegment StartX=103.5 StartY=34.7564 StartZ=0 EndX=103.5 EndY=20 EndZ=0
    g11: LineSegment StartX=103.5 StartY=20 StartZ=0 EndX=110 EndY=20 EndZ=0
    g12: ArcOfCircle CenterX=20 CenterY=20 CenterZ=0 NormalX=0 NormalY=0 NormalZ=1 AngleXU=0 Radius=20 StartAngle=2.31176 EndAngle=3.14159
    g13: ArcOfCircle CenterX=90 CenterY=20 CenterZ=0 NormalX=0 NormalY=0 NormalZ=1 AngleXU=0 Radius=20 StartAngle=7e-16 EndAngle=0.829832
  constraints (44):
    c: PointOnObject(g0,g-2)
    c: Horizontal(g0)
    c: Coincident(g0,g1)
    c: Vertical(g1)
    c: Coincident(g2,g3)
    c: Horizontal(g3)
    c: Coincident(g3,g4)
    c: Coincident(g4,g5)
    c: Horizontal(g5)
    c: Coincident(g6,g7)
    c: Coincident(g7,g8)
    c: Coincident(g8,g9)
    c: Coincident(g9,g6)
    c: Vertical(g10)
    c: Coincident(g10,g11)
    c: Horizontal(g11)
    c: Coincident(g12,g0)
    c: Coincident(g12,g1)
    c: Coincident(g13,g10)
    c: Coincident(g13,g11)
    c: Horizontal(g7)
    c: Horizontal(g9)
    c: Vertical(g8)
    c: Vertical(g6)
    c: Vertical(g4)
    c: Vertical(g2)
    c: Radius(g12) = 20
    c: Equal(g13,g12)
    c: DistanceX(g3,g3) = 6.5
    c: Equal(g0,g3)
    c: Equal(g3,g7)
    c: Equal(g7,g11)
    c: Horizontal(g0,g10)
    c: Horizontal(g6,g3)
    c: Equal(g4,g6)
    c: Perpendicular(g12,g0)
    c: Perpendicular(g13,g11)
    c: DistanceY(g-1,g0) = 20
    c: Coincident(g5,g2)
    c: Equal(g4,g5)
    c: DistanceX(g3,g6) = 23.5
    c: DistanceY(g-1,g8) = 40
    c: DistanceX(g-1,g2) = 36.75
    c: DistanceX(g0,g11) = 110
FEATURE [Sketcher::SketchObject] Sketch2661
  MapMode = 5
  Support = -> [XY_Plane1135]
  sketch-geometry (1):
    g0: Circle CenterX=0 CenterY=0 CenterZ=0 NormalX=0 NormalY=0 NormalZ=1 AngleXU=0 Radius=2.75
  constraints (2):
    c: Coincident(g0,g-1)
    c: Radius(g0) = 2.75
FEATURE [Sketcher::SketchObject] Sketch2662
  MapMode = 5
  Support = -> [XY_Plane1136]
  sketch-geometry (1):
    g0: Circle CenterX=0 CenterY=0 CenterZ=0 NormalX=0 NormalY=0 NormalZ=1 AngleXU=0 Radius=2.75
  constraints (2):
    c: Coincident(g0,g-1)
    c: Radius(g0) = 2.75
FEATURE [PartDesign::Pad] Pad1193  label="Baseplate049"
  Length = 160
  Length2 = 100
  Placement = pos=(0,0,0) rot=(1,0,0;1.5708rad)
  Profile = -> Sketch2652
  Reversed = true
  Type = 0
FEATURE [PartDesign::Thickness] Thickness003
  Base = -> Pad1193 [Face7,Face8,Face2]
  BaseFeature = -> Pad1193
  Join = 0
  Mode = 0
  Value = 2
FEATURE [PartDesign::Pad] Pad1195  label="Front Expansion001"
  BaseFeature = -> Thickness003
  Length = 23.75
  Length2 = 100
  Profile = -> Thickness003 [Face6]
  Type = 0
FEATURE [PartDesign::Pad] Pad1194  label="Rear Expansion001"
  BaseFeature = -> Pad1195
  Length = 23.75
  Length2 = 100
  Profile = -> Pad1195 [Face5]
  Type = 0
FEATURE [PartDesign::Pad] Pad1206  label="M3x8 Head191"
  Length = 3
  Length2 = 100
  Profile = -> Sketch2662
  Type = 0
FEATURE [Sketcher::SketchObject] Sketch2659
  MapMode = 5
  Placement = pos=(0,0,3) rot=(0,0,1;0rad)
  Support = -> [Pad1206]
  sketch-geometry (1):
    g0: Circle CenterX=0 CenterY=0 CenterZ=0 NormalX=0 NormalY=0 NormalZ=1 AngleXU=0 Radius=1.5
  constraints (2):
    c: Coincident(g0,g-1)
    c: Radius(g0) = 1.5
FEATURE [PartDesign::Pad] Pad1207  label="M3x8 Thread193"
  BaseFeature = -> Pad1206
  Length = 8
  Length2 = 100
  Profile = -> Sketch2659
  Type = 0
FEATURE [Sketcher::SketchObject] Sketch2657
  MapMode = 5
  Placement = pos=(0,0,0) rot=(1,0,0;3.14159rad)
  Support = -> [Pad1207]
  sketch-geometry (7):
    g0: LineSegment StartX=1.275 StartY=0.736122 StartZ=0 EndX=0 EndY=1.47224 EndZ=0
    g1: LineSegment StartX=0 StartY=1.47224 StartZ=0 EndX=-1.275 EndY=0.736122 EndZ=0
    g2: LineSegment StartX=-1.275 StartY=0.736122 StartZ=0 EndX=-1.275 EndY=-0.736122 EndZ=0
    g3: LineSegment StartX=-1.275 StartY=-0.736122 StartZ=0 EndX=1.34766e-11 EndY=-1.47224 EndZ=0
    g4: LineSegment StartX=1.34766e-11 StartY=-1.47224 StartZ=0 EndX=1.275 EndY=-0.736122 EndZ=0
    g5: LineSegment StartX=1.275 StartY=-0.736122 StartZ=0 EndX=1.275 EndY=0.736122 EndZ=0
    g6: Circle [constr] CenterX=0 CenterY=0 CenterZ=0 NormalX=0 NormalY=0 NormalZ=1 AngleXU=0 Radius=1.47224
  constraints (16):
    c: Coincident(g0,g1)
    c: Coincident(g1,g2)
    c: Coincident(g2,g3)
    c: Coincident(g3,g4)
    c: Coincident(g4,g5)
    c: Coincident(g5,g0)
    c: Equal(g0, g1-g5) x5
    c: PointOnObject(g0,g6)
    c: PointOnObject(g1,g6)
    c: PointOnObject(g2,g6)
    c: PointOnObject(g3,g6)
    c: PointOnObject(g4,g6)
    c: PointOnObject(g5,g6)
    c: Coincident(g6,g-1)
    c: PointOnObject(g0,g-2)
    c: DistanceX(g1,g0) = 2.55
FEATURE [PartDesign::Pocket] Pocket935  label="M3x8 Wrench191"
  BaseFeature = -> Pad1207
  Length = 1.3
  Length2 = 100
  Profile = -> Sketch2657
  Type = 0
FEATURE [PartDesign::Chamfer] Chamfer607  label="M3x8 Smooth190"
  Base = -> Pocket935 [Face11,Edge2,Edge24,Edge3]
  BaseFeature = -> Pocket935
  Size = 0.2
FEATURE [PartDesign::Pad] Pad1209  label="M3x8 Head193"
  Length = 3
  Length2 = 100
  Profile = -> Sketch2661
  Type = 0
FEATURE [Sketcher::SketchObject] Sketch2658
  MapMode = 5
  Placement = pos=(0,0,3) rot=(0,0,1;0rad)
  Support = -> [Pad1209]
  sketch-geometry (1):
    g0: Circle CenterX=0 CenterY=0 CenterZ=0 NormalX=0 NormalY=0 NormalZ=1 AngleXU=0 Radius=1.5
  constraints (2):
    c: Coincident(g0,g-1)
    c: Radius(g0) = 1.5
FEATURE [PartDesign::Pad] Pad1210  label="M3x8 Thread194"
  BaseFeature = -> Pad1209
  Length = 8
  Length2 = 100
  Profile = -> Sketch2658
  Type = 0
FEATURE [Sketcher::SketchObject] Sketch2660
  MapMode = 5
  Placement = pos=(0,0,0) rot=(1,0,0;3.14159rad)
  Support = -> [Pad1210]
  sketch-geometry (7):
    g0: LineSegment StartX=1.275 StartY=0.736122 StartZ=0 EndX=0 EndY=1.47224 EndZ=0
    g1: LineSegment StartX=0 StartY=1.47224 StartZ=0 EndX=-1.275 EndY=0.736122 EndZ=0
    g2: LineSegment StartX=-1.275 StartY=0.736122 StartZ=0 EndX=-1.275 EndY=-0.736122 EndZ=0
    g3: LineSegment StartX=-1.275 StartY=-0.736122 StartZ=0 EndX=1.34766e-11 EndY=-1.47224 EndZ=0
    g4: LineSegment StartX=1.34766e-11 StartY=-1.47224 StartZ=0 EndX=1.275 EndY=-0.736122 EndZ=0
    g5: LineSegment StartX=1.275 StartY=-0.736122 StartZ=0 EndX=1.275 EndY=0.736122 EndZ=0
    g6: Circle [constr] CenterX=0 CenterY=0 CenterZ=0 NormalX=0 NormalY=0 NormalZ=1 AngleXU=0 Radius=1.47224
  constraints (16):
    c: Coincident(g0,g1)
    c: Coincident(g1,g2)
    c: Coincident(g2,g3)
    c: Coincident(g3,g4)
    c: Coincident(g4,g5)
    c: Coincident(g5,g0)
    c: Equal(g0, g1-g5) x5
    c: PointOnObject(g0,g6)
    c: PointOnObject(g1,g6)
    c: PointOnObject(g2,g6)
    c: PointOnObject(g3,g6)
    c: PointOnObject(g4,g6)
    c: PointOnObject(g5,g6)
    c: Coincident(g6,g-1)
    c: PointOnObject(g0,g-2)
    c: DistanceX(g1,g0) = 2.55
FEATURE [PartDesign::Pocket] Pocket942  label="M3x8 Wrench192"
  BaseFeature = -> Pad1210
  Length = 1.3
  Length2 = 100
  Profile = -> Sketch2660
  Type = 0
FEATURE [PartDesign::Chamfer] Chamfer614  label="M3x8 Smooth193"
  Base = -> Pocket942 [Face11,Edge2,Edge24,Edge3]
  BaseFeature = -> Pocket942
  Size = 0.2
FEATURE [Sketcher::SketchObject] Sketch2663
  MapMode = 5
  Support = -> [XY_Plane1144]
  sketch-geometry (8):
    g0: LineSegment StartX=0 StartY=3.17543 StartZ=0 EndX=-2.75 EndY=1.58771 EndZ=0
    g1: LineSegment StartX=-2.75 StartY=1.58771 StartZ=0 EndX=-2.75 EndY=-1.58771 EndZ=0
    g2: LineSegment StartX=-2.75 StartY=-1.58771 StartZ=0 EndX=0 EndY=-3.17543 EndZ=0
    g3: LineSegment StartX=0 StartY=-3.17543 StartZ=0 EndX=2.75 EndY=-1.58771 EndZ=0
    g4: LineSegment StartX=2.75 StartY=-1.58771 StartZ=0 EndX=2.75 EndY=1.58771 EndZ=0
    g5: LineSegment StartX=2.75 StartY=1.58771 StartZ=0 EndX=0 EndY=3.17543 EndZ=0
    g6: Circle [constr] CenterX=0 CenterY=0 CenterZ=0 NormalX=0 NormalY=0 NormalZ=1 AngleXU=0 Radius=3.17543
    g7: Circle CenterX=0 CenterY=0 CenterZ=0 NormalX=0 NormalY=0 NormalZ=1 AngleXU=0 Radius=1.5
  constraints (18):
    c: Coincident(g0,g1)
    c: Coincident(g1,g2)
    c: Coincident(g2,g3)
    c: Coincident(g3,g4)
    c: Coincident(g4,g5)
    c: Coincident(g5,g0)
    c: Equal(g0, g1-g5) x5
    c: PointOnObject(g0,g6)
    c: PointOnObject(g1,g6)
    c: PointOnObject(g2,g6)
    c: PointOnObject(g3,g6)
    c: PointOnObject(g4,g6)
    c: PointOnObject(g5,g6)
    c: Coincident(g6,g-1)
    c: PointOnObject(g5,g-2)
    c: DistanceX(g0,g4) = 5.5
    c: Coincident(g7,g-1)
    c: Radius(g7) = 1.5
FEATURE [PartDesign::Pad] Pad1203  label="M3 Nut Primitive251"
  Length = 1.2
  Length2 = 1.2
  Profile = -> Sketch2663
  Type = 4
FEATURE [Sketcher::SketchObject] Sketch2664
  MapMode = 5
  Support = -> [XY_Plane1148]
  sketch-geometry (8):
    g0: LineSegment StartX=0 StartY=3.17543 StartZ=0 EndX=-2.75 EndY=1.58771 EndZ=0
    g1: LineSegment StartX=-2.75 StartY=1.58771 StartZ=0 EndX=-2.75 EndY=-1.58771 EndZ=0
    g2: LineSegment StartX=-2.75 StartY=-1.58771 StartZ=0 EndX=0 EndY=-3.17543 EndZ=0
    g3: LineSegment StartX=0 StartY=-3.17543 StartZ=0 EndX=2.75 EndY=-1.58771 EndZ=0
    g4: LineSegment StartX=2.75 StartY=-1.58771 StartZ=0 EndX=2.75 EndY=1.58771 EndZ=0
    g5: LineSegment StartX=2.75 StartY=1.58771 StartZ=0 EndX=0 EndY=3.17543 EndZ=0
    g6: Circle [constr] CenterX=0 CenterY=0 CenterZ=0 NormalX=0 NormalY=0 NormalZ=1 AngleXU=0 Radius=3.17543
    g7: Circle CenterX=0 CenterY=0 CenterZ=0 NormalX=0 NormalY=0 NormalZ=1 AngleXU=0 Radius=1.5
  constraints (18):
    c: Coincident(g0,g1)
    c: Coincident(g1,g2)
    c: Coincident(g2,g3)
    c: Coincident(g3,g4)
    c: Coincident(g4,g5)
    c: Coincident(g5,g0)
    c: Equal(g0, g1-g5) x5
    c: PointOnObject(g0,g6)
    c: PointOnObject(g1,g6)
    c: PointOnObject(g2,g6)
    c: PointOnObject(g3,g6)
    c: PointOnObject(g4,g6)
    c: PointOnObject(g5,g6)
    c: Coincident(g6,g-1)
    c: PointOnObject(g5,g-2)
    c: DistanceX(g0,g4) = 5.5
    c: Coincident(g7,g-1)
    c: Radius(g7) = 1.5
FEATURE [PartDesign::Pad] Pad1196  label="M3 Nut Primitive249"
  Length = 1.2
  Length2 = 1.2
  Profile = -> Sketch2664
  Type = 4
FEATURE [Sketcher::SketchObject] Sketch2666
  MapMode = 5
  Support = -> [XY_Plane1142]
  sketch-geometry (8):
    g0: LineSegment StartX=0 StartY=3.17543 StartZ=0 EndX=-2.75 EndY=1.58771 EndZ=0
    g1: LineSegment StartX=-2.75 StartY=1.58771 StartZ=0 EndX=-2.75 EndY=-1.58771 EndZ=0
    g2: LineSegment StartX=-2.75 StartY=-1.58771 StartZ=0 EndX=0 EndY=-3.17543 EndZ=0
    g3: LineSegment StartX=0 StartY=-3.17543 StartZ=0 EndX=2.75 EndY=-1.58771 EndZ=0
    g4: LineSegment StartX=2.75 StartY=-1.58771 StartZ=0 EndX=2.75 EndY=1.58771 EndZ=0
    g5: LineSegment StartX=2.75 StartY=1.58771 StartZ=0 EndX=0 EndY=3.17543 EndZ=0
    g6: Circle [constr] CenterX=0 CenterY=0 CenterZ=0 NormalX=0 NormalY=0 NormalZ=1 AngleXU=0 Radius=3.17543
    g7: Circle CenterX=0 CenterY=0 CenterZ=0 NormalX=0 NormalY=0 NormalZ=1 AngleXU=0 Radius=1.5
  constraints (18):
    c: Coincident(g0,g1)
    c: Coincident(g1,g2)
    c: Coincident(g2,g3)
    c: Coincident(g3,g4)
    c: Coincident(g4,g5)
    c: Coincident(g5,g0)
    c: Equal(g0, g1-g5) x5
    c: PointOnObject(g0,g6)
    c: PointOnObject(g1,g6)
    c: PointOnObject(g2,g6)
    c: PointOnObject(g3,g6)
    c: PointOnObject(g4,g6)
    c: PointOnObject(g5,g6)
    c: Coincident(g6,g-1)
    c: PointOnObject(g5,g-2)
    c: DistanceX(g0,g4) = 5.5
    c: Coincident(g7,g-1)
    c: Radius(g7) = 1.5
FEATURE [PartDesign::Pad] Pad1205  label="M3 Nut Primitive252"
  Length = 1.2
  Length2 = 1.2
  Profile = -> Sketch2666
  Type = 4
FEATURE [Sketcher::SketchObject] Sketch2665
  ExternalGeometry = -> [Pad1205]
  MapMode = 5
  Placement = pos=(0,0,0) rot=(0.57735,0.57735,0.57735;2.0944rad)
  Support = -> [YZ_Plane1137]
  sketch-geometry (6):
    g0: LineSegment StartX=-2.67543 StartY=1.2 StartZ=0 EndX=-3.67543 EndY=1.2 EndZ=0
    g1: LineSegment StartX=-3.67543 StartY=1.2 StartZ=0 EndX=-3.67543 EndY=-1.2 EndZ=0
    g2: LineSegment StartX=-3.67543 StartY=-1.2 StartZ=0 EndX=-2.67543 EndY=-1.2 EndZ=0
    g3: LineSegment StartX=-2.67543 StartY=-1.2 StartZ=0 EndX=-3.17543 EndY=-1 EndZ=0
    g4: LineSegment StartX=-3.17543 StartY=-1 StartZ=0 EndX=-3.17543 EndY=1 EndZ=0
    g5: LineSegment StartX=-3.17543 StartY=1 StartZ=0 EndX=-2.67543 EndY=1.2 EndZ=0
  constraints (15):
    c: Horizontal(g0)
    c: Coincident(g0,g1)
    c: Coincident(g1,g2)
    c: Coincident(g2,g3)
    c: Coincident(g3,g4)
    c: Coincident(g4,g5)
    c: Coincident(g5,g0)
    c: Symmetric(g4,g3,g-1)
    c: Symmetric(g0,g2,g-1)
    c: Symmetric(g1,g0,g-1)
    c: DistanceX(g0,g4) = 0.5
    c: DistanceY(g3,g4) = 2
    c: DistanceY(g1,g0) = 2.4
    c: PointOnObject(g3,g-3)
    c: DistanceX(g4,g0) = 0.5
FEATURE [PartDesign::Groove] Groove259  label="M3 Nut Smooth250"
  Angle = 360
  Axis = (-2e-16,3e-16,1)
  Base = (0,0,0)
  BaseFeature = -> Pad1205
  Profile = -> Sketch2665
  ReferenceAxis = -> Sketch2665 [V_Axis]
  Reversed = true
FEATURE [PartDesign::Chamfer] Chamfer611  label="M3 Nut Smooth Hole251"
  Base = -> Groove259 [Edge24,Edge23]
  BaseFeature = -> Groove259
  Size = 0.2
FEATURE [PartDesign::Body] Body801  label="M3 Nut149"
  Group = -> [Sketch2666,Pad1205,Sketch2665,Groove259,Chamfer611]
  Origin = -> Origin1140
  Placement = pos=(36.75,13.5,0) rot=(0,0,1;0rad)
  Tip = -> Chamfer611
FEATURE [Sketcher::SketchObject] Sketch2667
  MapMode = 5
  Support = -> [XY_Plane1145]
  sketch-geometry (8):
    g0: LineSegment StartX=0 StartY=3.17543 StartZ=0 EndX=-2.75 EndY=1.58771 EndZ=0
    g1: LineSegment StartX=-2.75 StartY=1.58771 StartZ=0 EndX=-2.75 EndY=-1.58771 EndZ=0
    g2: LineSegment StartX=-2.75 StartY=-1.58771 StartZ=0 EndX=0 EndY=-3.17543 EndZ=0
    g3: LineSegment StartX=0 StartY=-3.17543 StartZ=0 EndX=2.75 EndY=-1.58771 EndZ=0
    g4: LineSegment StartX=2.75 StartY=-1.58771 StartZ=0 EndX=2.75 EndY=1.58771 EndZ=0
    g5: LineSegment StartX=2.75 StartY=1.58771 StartZ=0 EndX=0 EndY=3.17543 EndZ=0
    g6: Circle [constr] CenterX=0 CenterY=0 CenterZ=0 NormalX=0 NormalY=0 NormalZ=1 AngleXU=0 Radius=3.17543
    g7: Circle CenterX=0 CenterY=0 CenterZ=0 NormalX=0 NormalY=0 NormalZ=1 AngleXU=0 Radius=1.5
  constraints (18):
    c: Coincident(g0,g1)
    c: Coincident(g1,g2)
    c: Coincident(g2,g3)
    c: Coincident(g3,g4)
    c: Coincident(g4,g5)
    c: Coincident(g5,g0)
    c: Equal(g0, g1-g5) x5
    c: PointOnObject(g0,g6)
    c: PointOnObject(g1,g6)
    c: PointOnObject(g2,g6)
    c: PointOnObject(g3,g6)
    c: PointOnObject(g4,g6)
    c: PointOnObject(g5,g6)
    c: Coincident(g6,g-1)
    c: PointOnObject(g5,g-2)
    c: DistanceX(g0,g4) = 5.5
    c: Coincident(g7,g-1)
    c: Radius(g7) = 1.5
FEATURE [PartDesign::Pad] Pad1197  label="M3 Nut Primitive250"
  Length = 1.2
  Length2 = 1.2
  Profile = -> Sketch2667
  Type = 4
FEATURE [Sketcher::SketchObject] Sketch2668
  ExternalGeometry = -> [Pad1197]
  MapMode = 5
  Placement = pos=(0,0,0) rot=(0.57735,0.57735,0.57735;2.0944rad)
  Support = -> [YZ_Plane1139]
  sketch-geometry (6):
    g0: LineSegment StartX=-2.67543 StartY=1.2 StartZ=0 EndX=-3.67543 EndY=1.2 EndZ=0
    g1: LineSegment StartX=-3.67543 StartY=1.2 StartZ=0 EndX=-3.67543 EndY=-1.2 EndZ=0
    g2: LineSegment StartX=-3.67543 StartY=-1.2 StartZ=0 EndX=-2.67543 EndY=-1.2 EndZ=0
    g3: LineSegment StartX=-2.67543 StartY=-1.2 StartZ=0 EndX=-3.17543 EndY=-1 EndZ=0
    g4: LineSegment StartX=-3.17543 StartY=-1 StartZ=0 EndX=-3.17543 EndY=1 EndZ=0
    g5: LineSegment StartX=-3.17543 StartY=1 StartZ=0 EndX=-2.67543 EndY=1.2 EndZ=0
  constraints (15):
    c: Horizontal(g0)
    c: Coincident(g0,g1)
    c: Coincident(g1,g2)
    c: Coincident(g2,g3)
    c: Coincident(g3,g4)
    c: Coincident(g4,g5)
    c: Coincident(g5,g0)
    c: Symmetric(g4,g3,g-1)
    c: Symmetric(g0,g2,g-1)
    c: Symmetric(g1,g0,g-1)
    c: DistanceX(g0,g4) = 0.5
    c: DistanceY(g3,g4) = 2
    c: DistanceY(g1,g0) = 2.4
    c: PointOnObject(g3,g-3)
    c: DistanceX(g4,g0) = 0.5
FEATURE [PartDesign::Groove] Groove258  label="M3 Nut Smooth249"
  Angle = 360
  Axis = (-2e-16,3e-16,1)
  Base = (0,0,0)
  BaseFeature = -> Pad1197
  Profile = -> Sketch2668
  ReferenceAxis = -> Sketch2668 [V_Axis]
  Reversed = true
FEATURE [PartDesign::Chamfer] Chamfer612  label="M3 Nut Smooth Hole252"
  Base = -> Groove258 [Edge24,Edge23]
  BaseFeature = -> Groove258
  Size = 0.2
FEATURE [PartDesign::Body] Body805  label="M3 Nut152"
  Group = -> [Sketch2667,Pad1197,Sketch2668,Groove258,Chamfer612]
  Origin = -> Origin1138
  Placement = pos=(103.5,0,0) rot=(0,0,1;0rad)
  Tip = -> Chamfer612
FEATURE [Sketcher::SketchObject] Sketch2671
  ExternalGeometry = -> [Pad1196]
  MapMode = 5
  Placement = pos=(0,0,0) rot=(0.57735,0.57735,0.57735;2.0944rad)
  Support = -> [YZ_Plane1138]
  sketch-geometry (6):
    g0: LineSegment StartX=-2.67543 StartY=1.2 StartZ=0 EndX=-3.67543 EndY=1.2 EndZ=0
    g1: LineSegment StartX=-3.67543 StartY=1.2 StartZ=0 EndX=-3.67543 EndY=-1.2 EndZ=0
    g2: LineSegment StartX=-3.67543 StartY=-1.2 StartZ=0 EndX=-2.67543 EndY=-1.2 EndZ=0
    g3: LineSegment StartX=-2.67543 StartY=-1.2 StartZ=0 EndX=-3.17543 EndY=-1 EndZ=0
    g4: LineSegment StartX=-3.17543 StartY=-1 StartZ=0 EndX=-3.17543 EndY=1 EndZ=0
    g5: LineSegment StartX=-3.17543 StartY=1 StartZ=0 EndX=-2.67543 EndY=1.2 EndZ=0
  constraints (15):
    c: Horizontal(g0)
    c: Coincident(g0,g1)
    c: Coincident(g1,g2)
    c: Coincident(g2,g3)
    c: Coincident(g3,g4)
    c: Coincident(g4,g5)
    c: Coincident(g5,g0)
    c: Symmetric(g4,g3,g-1)
    c: Symmetric(g0,g2,g-1)
    c: Symmetric(g1,g0,g-1)
    c: DistanceX(g0,g4) = 0.5
    c: DistanceY(g3,g4) = 2
    c: DistanceY(g1,g0) = 2.4
    c: PointOnObject(g3,g-3)
    c: DistanceX(g4,g0) = 0.5
FEATURE [PartDesign::Groove] Groove261  label="M3 Nut Smooth252"
  Angle = 360
  Axis = (-2e-16,3e-16,1)
  Base = (0,0,0)
  BaseFeature = -> Pad1196
  Profile = -> Sketch2671
  ReferenceAxis = -> Sketch2671 [V_Axis]
  Reversed = true
FEATURE [PartDesign::Chamfer] Chamfer609  label="M3 Nut Smooth Hole249"
  Base = -> Groove261 [Edge24,Edge23]
  BaseFeature = -> Groove261
  Size = 0.2
FEATURE [PartDesign::Body] Body802  label="M3 Nut150"
  Group = -> [Sketch2664,Pad1196,Sketch2671,Groove261,Chamfer609]
  Origin = -> Origin1137
  Placement = pos=(66.75,13.5,0) rot=(0,0,1;0rad)
  Tip = -> Chamfer609
FEATURE [Sketcher::SketchObject] Sketch2674
  ExternalGeometry = -> [Pad1203]
  MapMode = 5
  Placement = pos=(0,0,0) rot=(0.57735,0.57735,0.57735;2.0944rad)
  Support = -> [YZ_Plane1141]
  sketch-geometry (6):
    g0: LineSegment StartX=-2.67543 StartY=1.2 StartZ=0 EndX=-3.67543 EndY=1.2 EndZ=0
    g1: LineSegment StartX=-3.67543 StartY=1.2 StartZ=0 EndX=-3.67543 EndY=-1.2 EndZ=0
    g2: LineSegment StartX=-3.67543 StartY=-1.2 StartZ=0 EndX=-2.67543 EndY=-1.2 EndZ=0
    g3: LineSegment StartX=-2.67543 StartY=-1.2 StartZ=0 EndX=-3.17543 EndY=-1 EndZ=0
    g4: LineSegment StartX=-3.17543 StartY=-1 StartZ=0 EndX=-3.17543 EndY=1 EndZ=0
    g5: LineSegment StartX=-3.17543 StartY=1 StartZ=0 EndX=-2.67543 EndY=1.2 EndZ=0
  constraints (15):
    c: Horizontal(g0)
    c: Coincident(g0,g1)
    c: Coincident(g1,g2)
    c: Coincident(g2,g3)
    c: Coincident(g3,g4)
    c: Coincident(g4,g5)
    c: Coincident(g5,g0)
    c: Symmetric(g4,g3,g-1)
    c: Symmetric(g0,g2,g-1)
    c: Symmetric(g1,g0,g-1)
    c: DistanceX(g0,g4) = 0.5
    c: DistanceY(g3,g4) = 2
    c: DistanceY(g1,g0) = 2.4
    c: PointOnObject(g3,g-3)
    c: DistanceX(g4,g0) = 0.5
FEATURE [PartDesign::Groove] Groove260  label="M3 Nut Smooth251"
  Angle = 360
  Axis = (-2e-16,3e-16,1)
  Base = (0,0,0)
  BaseFeature = -> Pad1203
  Profile = -> Sketch2674
  ReferenceAxis = -> Sketch2674 [V_Axis]
  Reversed = true
FEATURE [PartDesign::Chamfer] Chamfer610  label="M3 Nut Smooth Hole250"
  Base = -> Groove260 [Edge24,Edge23]
  BaseFeature = -> Groove260
  Size = 0.2
FEATURE [PartDesign::Body] Body803  label="M3 Nut151"
  Group = -> [Sketch2663,Pad1203,Sketch2674,Groove260,Chamfer610]
  Origin = -> Origin1148
  Tip = -> Chamfer610
FEATURE [Sketcher::SketchObject] Sketch2676
  AttachmentOffset = pos=(0,0,-108.85) rot=(0,0,1;0rad)
  MapMode = 5
  Placement = pos=(0,108.85,2.42e-14) rot=(1,0,0;1.5708rad)
  Support = -> [XZ_Plane1145]
  sketch-geometry (14):
    g0: LineSegment StartX=0 StartY=20 StartZ=0 EndX=6.5 EndY=20 EndZ=0
    g1: LineSegment StartX=6.5 StartY=20 StartZ=0 EndX=6.5 EndY=34.7564 EndZ=0
    g2: LineSegment StartX=36.75 StartY=40 StartZ=0 EndX=36.75 EndY=33.5 EndZ=0
    g3: LineSegment StartX=36.75 StartY=33.5 StartZ=0 EndX=43.25 EndY=33.5 EndZ=0
    g4: LineSegment StartX=43.25 StartY=33.5 StartZ=0 EndX=43.25 EndY=40 EndZ=0
    g5: LineSegment StartX=43.25 StartY=40 StartZ=0 EndX=36.75 EndY=40 EndZ=0
    g6: LineSegment StartX=66.75 StartY=40 StartZ=0 EndX=66.75 EndY=33.5 EndZ=0
    g7: LineSegment StartX=66.75 StartY=33.5 StartZ=0 EndX=73.25 EndY=33.5 EndZ=0
    g8: LineSegment StartX=73.25 StartY=33.5 StartZ=0 EndX=73.25 EndY=40 EndZ=0
    g9: LineSegment StartX=73.25 StartY=40 StartZ=0 EndX=66.75 EndY=40 EndZ=0
    g10: LineSegment StartX=103.5 StartY=34.7564 StartZ=0 EndX=103.5 EndY=20 EndZ=0
    g11: LineSegment StartX=103.5 StartY=20 StartZ=0 EndX=110 EndY=20 EndZ=0
    g12: ArcOfCircle CenterX=20 CenterY=20 CenterZ=0 NormalX=0 NormalY=0 NormalZ=1 AngleXU=0 Radius=20 StartAngle=2.31176 EndAngle=3.14159
    g13: ArcOfCircle CenterX=90 CenterY=20 CenterZ=0 NormalX=0 NormalY=0 NormalZ=1 AngleXU=0 Radius=20 StartAngle=7e-16 EndAngle=0.829832
  constraints (44):
    c: PointOnObject(g0,g-2)
    c: Horizontal(g0)
    c: Coincident(g0,g1)
    c: Vertical(g1)
    c: Coincident(g2,g3)
    c: Horizontal(g3)
    c: Coincident(g3,g4)
    c: Coincident(g4,g5)
    c: Horizontal(g5)
    c: Coincident(g6,g7)
    c: Coincident(g7,g8)
    c: Coincident(g8,g9)
    c: Coincident(g9,g6)
    c: Vertical(g10)
    c: Coincident(g10,g11)
    c: Horizontal(g11)
    c: Coincident(g12,g0)
    c: Coincident(g12,g1)
    c: Coincident(g13,g10)
    c: Coincident(g13,g11)
    c: Horizontal(g7)
    c: Horizontal(g9)
    c: Vertical(g8)
    c: Vertical(g6)
    c: Vertical(g4)
    c: Vertical(g2)
    c: Radius(g12) = 20
    c: Equal(g13,g12)
    c: DistanceX(g3,g3) = 6.5
    c: Equal(g0,g3)
    c: Equal(g3,g7)
    c: Equal(g7,g11)
    c: Horizontal(g0,g10)
    c: Horizontal(g6,g3)
    c: Equal(g4,g6)
    c: Perpendicular(g12,g0)
    c: Perpendicular(g13,g11)
    c: DistanceY(g-1,g0) = 20
    c: Coincident(g5,g2)
    c: Equal(g4,g5)
    c: DistanceX(g3,g6) = 23.5
    c: DistanceY(g-1,g8) = 40
    c: DistanceX(g-1,g2) = 36.75
    c: DistanceX(g0,g11) = 110
FEATURE [Sketcher::SketchObject] Sketch2679
  MapMode = 5
  Placement = pos=(0,0,0) rot=(1,0,0;1.5708rad)
  Support = -> [XZ_Plane1145]
  sketch-geometry (6):
    g0: LineSegment StartX=20 StartY=40 StartZ=0 EndX=90 EndY=40 EndZ=0
    g1: LineSegment StartX=110 StartY=20 StartZ=0 EndX=110 EndY=0 EndZ=0
    g2: LineSegment StartX=110 StartY=0 StartZ=0 EndX=0 EndY=0 EndZ=0
    g3: LineSegment StartX=0 StartY=0 StartZ=0 EndX=0 EndY=20 EndZ=0
    g4: ArcOfCircle CenterX=20 CenterY=20 CenterZ=0 NormalX=0 NormalY=0 NormalZ=1 AngleXU=0 Radius=20 StartAngle=1.5708 EndAngle=3.14159
    g5: ArcOfCircle CenterX=90 CenterY=20 CenterZ=0 NormalX=0 NormalY=0 NormalZ=1 AngleXU=0 Radius=20 StartAngle=0 EndAngle=1.5708
  constraints (15):
    c: Coincident(g1,g2)
    c: Coincident(g2,g3)
    c: Horizontal(g0)
    c: Horizontal(g2)
    c: Vertical(g1)
    c: Vertical(g3)
    c: Tangent(g3,g4) = 1.5708
    c: Tangent(g0,g4) = 1.5708
    c: Tangent(g0,g5) = 1.5708
    c: Tangent(g1,g5) = 1.5708
    c: DistanceX(g2,g2) = 110
    c: Equal(g5,g4)
    c: Radius(g4) = 20
    c: Coincident(g2,g-1)
    c: DistanceY(g2,g0) = 40
FEATURE [PartDesign::Pad] Pad1199  label="Baseplate050"
  Length = 160
  Length2 = 100
  Placement = pos=(0,0,0) rot=(1,0,0;1.5708rad)
  Profile = -> Sketch2679
  Reversed = true
  Type = 0
FEATURE [PartDesign::Thickness] Thickness002
  Base = -> Pad1199 [Face7,Face8,Face2]
  BaseFeature = -> Pad1199
  Join = 0
  Mode = 0
  Value = 2
FEATURE [PartDesign::Pad] Pad1200  label="Front Expansion002"
  BaseFeature = -> Thickness002
  Length = 23.75
  Length2 = 100
  Profile = -> Thickness002 [Face6]
  Type = 0
FEATURE [PartDesign::Pad] Pad1204  label="Rear Expansion002"
  BaseFeature = -> Pad1200
  Length = 23.75
  Length2 = 100
  Profile = -> Pad1200 [Face5]
  Type = 0
FEATURE [Sketcher::SketchObject] Sketch2675
  MapMode = 5
  Placement = pos=(0,-9.2e-15,42) rot=(0,0,1;0rad)
  Support = -> [Pad1204]
  sketch-geometry (16):
    g0: LineSegment StartX=-2 StartY=0 StartZ=0 EndX=30 EndY=0 EndZ=0
    g1: LineSegment StartX=30 StartY=0 StartZ=0 EndX=30 EndY=-23.75 EndZ=0
    g2: LineSegment StartX=30 StartY=-23.75 StartZ=0 EndX=-2 EndY=-23.75 EndZ=0
    g3: LineSegment StartX=-2 StartY=-23.75 StartZ=0 EndX=-2 EndY=0 EndZ=0
    g4: LineSegment StartX=112 StartY=0 StartZ=0 EndX=80 EndY=0 EndZ=0
    g5: LineSegment StartX=80 StartY=0 StartZ=0 EndX=80 EndY=-23.75 EndZ=0
    g6: LineSegment StartX=80 StartY=-23.75 StartZ=0 EndX=112 EndY=-23.75 EndZ=0
    g7: LineSegment StartX=112 StartY=-23.75 StartZ=0 EndX=112 EndY=0 EndZ=0
    g8: LineSegment StartX=-2 StartY=160 StartZ=0 EndX=30 EndY=160 EndZ=0
    g9: LineSegment StartX=30 StartY=160 StartZ=0 EndX=30 EndY=183.75 EndZ=0
    g10: LineSegment StartX=30 StartY=183.75 StartZ=0 EndX=-2 EndY=183.75 EndZ=0
    g11: LineSegment StartX=-2 StartY=183.75 StartZ=0 EndX=-2 EndY=160 EndZ=0
    g12: LineSegment StartX=112 StartY=183.75 StartZ=0 EndX=80 EndY=183.75 EndZ=0
    g13: LineSegment StartX=80 StartY=183.75 StartZ=0 EndX=80 EndY=160 EndZ=0
    g14: LineSegment StartX=80 StartY=160 StartZ=0 EndX=112 EndY=160 EndZ=0
    g15: LineSegment StartX=112 StartY=160 StartZ=0 EndX=112 EndY=183.75 EndZ=0
  constraints (48):
    c: Coincident(g0,g1)
    c: Coincident(g1,g2)
    c: Coincident(g2,g3)
    c: Coincident(g3,g0)
    c: Horizontal(g0)
    c: Horizontal(g2)
    c: Vertical(g1)
    c: Vertical(g3)
    c: PointOnObject(g0,g-1)
    c: Coincident(g4,g5)
    c: Coincident(g5,g6)
    c: Coincident(g6,g7)
    c: Coincident(g7,g4)
    c: Horizontal(g4)
    c: Horizontal(g6)
    c: Vertical(g5)
    c: Vertical(g7)
    c: Coincident(g8,g9)
    c: Coincident(g9,g10)
    c: Coincident(g10,g11)
    c: Coincident(g11,g8)
    c: Horizontal(g8)
    c: Horizontal(g10)
    c: Vertical(g9)
    c: Vertical(g11)
    c: Coincident(g12,g13)
    c: Coincident(g13,g14)
    c: Coincident(g14,g15)
    c: Coincident(g15,g12)
    c: Horizontal(g12)
    c: Horizontal(g14)
    c: Vertical(g13)
    c: Vertical(g15)
    c: Horizontal(g9,g12)
    c: Equal(g9,g13)
    c: Equal(g10,g12)
    c: Equal(g0,g8)
    c: Equal(g4,g14)
    c: Horizontal(g0,g4)
    c: Equal(g5,g1)
    c: DistanceX(g0,g4) = 50
    c: DistanceX(g0,g0) = 32
    c: DistanceY(g3,g3) = 23.75
    c: DistanceX(g0,g-1) = 2
    c: Vertical(g0,g8)
    c: Vertical(g13,g4)
    c: DistanceY(g0,g8) = 160
    c: Equal(g9,g1)
FEATURE [PartDesign::Pocket] Pocket936  label="Shoulders002"
  BaseFeature = -> Pad1204
  Length = 42
  Length2 = 100
  Profile = -> Sketch2675
  Type = 0
FEATURE [Sketcher::SketchObject] Sketch2681
  MapMode = 5
  Placement = pos=(112,0,0) rot=(0.57735,0.57735,0.57735;2.0944rad)
  Support = -> [Pocket936]
  sketch-geometry (6):
    g0: LineSegment StartX=0 StartY=-5 StartZ=0 EndX=-2e-16 EndY=12 EndZ=0
    g1: LineSegment StartX=-2e-16 StartY=12 StartZ=0 EndX=75 EndY=12 EndZ=0
    g2: LineSegment StartX=75 StartY=12 StartZ=0 EndX=105 EndY=0 EndZ=0
    g3: LineSegment StartX=105 StartY=0 StartZ=0 EndX=160 EndY=0 EndZ=0
    g4: LineSegment StartX=160 StartY=0 StartZ=0 EndX=160 EndY=-5 EndZ=0
    g5: LineSegment StartX=160 StartY=-5 StartZ=0 EndX=0 EndY=-5 EndZ=0
  constraints (18):
    c: PointOnObject(g0,g-2)
    c: Coincident(g0,g1)
    c: Horizontal(g1)
    c: Coincident(g1,g2)
    c: PointOnObject(g2,g-1)
    c: Coincident(g2,g3)
    c: Horizontal(g3)
    c: Coincident(g3,g4)
    c: Vertical(g4)
    c: Coincident(g4,g5)
    c: PointOnObject(g5,g-2)
    c: Horizontal(g5)
    c: Coincident(g0,g5)
    c: DistanceX(g1,g2) = 30
    c: DistanceX(g5,g5) = 160
    c: DistanceX(g1,g1) = 75
    c: DistanceY(g-1,g0) = 12
    c: DistanceY(g4,g4) = 5
FEATURE [PartDesign::Pocket] Pocket941  label="Side Detailing002"
  BaseFeature = -> Pocket936
  Length = 114
  Length2 = 100
  Profile = -> Sketch2681
  Type = 0
FEATURE [Sketcher::SketchObject] Sketch2670
  MapMode = 5
  Placement = pos=(0,-9.2e-15,42) rot=(0,0,1;0rad)
  Support = -> [Pocket941]
  sketch-geometry (4):
    g0: Circle CenterX=40 CenterY=-18.75 CenterZ=0 NormalX=0 NormalY=0 NormalZ=1 AngleXU=0 Radius=1.6
    g1: Circle CenterX=70 CenterY=-18.75 CenterZ=0 NormalX=0 NormalY=0 NormalZ=1 AngleXU=0 Radius=1.6
    g2: Circle CenterX=40 CenterY=178.75 CenterZ=0 NormalX=0 NormalY=0 NormalZ=1 AngleXU=0 Radius=1.6
    g3: Circle CenterX=70 CenterY=178.75 CenterZ=0 NormalX=0 NormalY=0 NormalZ=1 AngleXU=0 Radius=1.6
  constraints (12):
    c: DistanceX(g2,g3) = 30
    c: Equal(g2,g3)
    c: Equal(g3,g0)
    c: Equal(g0,g1)
    c: Horizontal(g2,g3)
    c: Horizontal(g0,g1)
    c: Vertical(g1,g3)
    c: Vertical(g0,g2)
    c: DistanceY(g0,g-1) = 18.75
    c: DistanceX(g-1,g0) = 40
    c: DistanceY(g-1,g2) = 178.75
    c: Radius(g3) = 1.6
FEATURE [PartDesign::Pocket] Pocket938  label="Screwholes013"
  BaseFeature = -> Pocket941
  Length = 2
  Length2 = 100
  Profile = -> Sketch2670
  Type = 0
FEATURE [PartDesign::Fillet] Fillet275  label="Round Corners002"
  Base = -> Pocket938 [Edge35,Edge66,Edge48,Edge12,Edge18,Edge44,Edge25,Edge76,Edge57,Edge60,Edge45,Edge9]
  BaseFeature = -> Pocket938
  Radius = 5
FEATURE [PartDesign::Fillet] Fillet273  label="Round Side Details002"
  Base = -> Fillet275 [Edge21,Edge29,Edge131,Edge132]
  BaseFeature = -> Fillet275
  Radius = 20
FEATURE [PartDesign::Pad] Pad1202  label="Screwpads002"
  BaseFeature = -> Fillet273
  Length = 5.5
  Length2 = 5.5
  Profile = -> Sketch2676
  Type = 4
FEATURE [PartDesign::Fillet] Fillet276  label="Smooth Screwpad Edges002"
  Base = -> Pad1202 [Edge35,Edge33,Edge137,Edge141,Edge145,Edge149,Edge182,Edge77,Edge73,Edge71,Edge75,Edge123]
  BaseFeature = -> Pad1202
  Radius = 1
FEATURE [PartDesign::Fillet] Fillet274  label="Smooth Screwpad Edges Side Details002"
  Base = -> Fillet276 [Edge23,Edge202]
  BaseFeature = -> Fillet276
  Radius = 0.2
FEATURE [Sketcher::SketchObject] Sketch2672
  MapMode = 5
  Placement = pos=(-8.12e-14,114.35,8.35e-14) rot=(0,0.707107,0.707107;3.14159rad)
  Support = -> [Fillet274]
  sketch-geometry (4):
    g0: Circle CenterX=-106.75 CenterY=23.25 CenterZ=0 NormalX=0 NormalY=0 NormalZ=1 AngleXU=0 Radius=1.6
    g1: Circle CenterX=-70 CenterY=36.75 CenterZ=0 NormalX=0 NormalY=0 NormalZ=1 AngleXU=0 Radius=1.6
    g2: Circle CenterX=-40 CenterY=36.75 CenterZ=0 NormalX=0 NormalY=0 NormalZ=1 AngleXU=0 Radius=1.6
    g3: Circle CenterX=-3.25 CenterY=23.25 CenterZ=0 NormalX=0 NormalY=0 NormalZ=1 AngleXU=0 Radius=1.6
  constraints (12):
    c: Equal(g0,g1)
    c: Equal(g1,g2)
    c: Equal(g2,g3)
    c: DistanceX(g1,g2) = 30
    c: DistanceX(g3,g-1) = 3.25
    c: DistanceY(g-1,g3) = 23.25
    c: DistanceX(g0,g3) = 103.5
    c: Horizontal(g3,g0)
    c: Horizontal(g1,g2)
    c: DistanceX(g2,g-1) = 40
    c: DistanceY(g-1,g2) = 36.75
    c: Radius(g3) = 1.6
FEATURE [PartDesign::Pocket] Pocket940  label="Screwholes Connection002"
  BaseFeature = -> Fillet274
  Length = 11
  Length2 = 100
  Profile = -> Sketch2672
  Type = 0
FEATURE [Sketcher::SketchObject] Sketch2680
  MapMode = 5
  Placement = pos=(-8.12e-14,114.35,8.35e-14) rot=(0,0.707107,0.707107;3.14159rad)
  Support = -> [Pocket940]
  sketch-geometry (4):
    g0: Circle CenterX=-106.75 CenterY=23.25 CenterZ=0 NormalX=0 NormalY=0 NormalZ=1 AngleXU=0 Radius=2.85
    g1: Circle CenterX=-70 CenterY=36.75 CenterZ=0 NormalX=0 NormalY=0 NormalZ=1 AngleXU=0 Radius=2.85
    g2: Circle CenterX=-40 CenterY=36.75 CenterZ=0 NormalX=0 NormalY=0 NormalZ=1 AngleXU=0 Radius=2.85
    g3: Circle CenterX=-3.25 CenterY=23.25 CenterZ=0 NormalX=0 NormalY=0 NormalZ=1 AngleXU=0 Radius=2.85
  constraints (12):
    c: Equal(g0,g1)
    c: Equal(g1,g2)
    c: Equal(g2,g3)
    c: Radius(g3) = 2.85
    c: DistanceX(g3,g-1) = 3.25
    c: Horizontal(g3,g0)
    c: Horizontal(g1,g2)
    c: DistanceX(g0,g3) = 103.5
    c: DistanceX(g1,g2) = 30
    c: DistanceY(g-1,g2) = 36.75
    c: DistanceX(g2,g-1) = 40
    c: DistanceY(g-1,g3) = 23.25
FEATURE [PartDesign::Pocket] Pocket934  label="Screwheads Connection002"
  BaseFeature = -> Pocket940
  Length = 3
  Length2 = 100
  Profile = -> Sketch2680
  Type = 0
FEATURE [Sketcher::SketchObject] Sketch2677
  MapMode = 5
  Placement = pos=(7.34e-14,103.35,7.54e-14) rot=(1,0,0;1.5708rad)
  Support = -> [Pocket934]
  sketch-geometry (28):
    g0: LineSegment StartX=3.25 StartY=26.5409 StartZ=0 EndX=0.4 EndY=24.8954 EndZ=0
    g1: LineSegment StartX=0.4 StartY=24.8954 StartZ=0 EndX=0.4 EndY=21.6046 EndZ=0
    g2: LineSegment StartX=0.4 StartY=21.6046 StartZ=0 EndX=3.25 EndY=19.9591 EndZ=0
    g3: LineSegment StartX=3.25 StartY=19.9591 StartZ=0 EndX=6.1 EndY=21.6046 EndZ=0
    g4: LineSegment StartX=6.1 StartY=21.6046 StartZ=0 EndX=6.1 EndY=24.8954 EndZ=0
    g5: LineSegment StartX=6.1 StartY=24.8954 StartZ=0 EndX=3.25 EndY=26.5409 EndZ=0
    g6: Circle [constr] CenterX=3.25 CenterY=23.25 CenterZ=0 NormalX=0 NormalY=0 NormalZ=1 AngleXU=0 Radius=3.2909
    g7: LineSegment StartX=40 StartY=40.0409 StartZ=0 EndX=37.15 EndY=38.3954 EndZ=0
    g8: LineSegment StartX=37.15 StartY=38.3954 StartZ=0 EndX=37.15 EndY=35.1046 EndZ=0
    g9: LineSegment StartX=37.15 StartY=35.1046 StartZ=0 EndX=40 EndY=33.4591 EndZ=0
    g10: LineSegment StartX=40 StartY=33.4591 StartZ=0 EndX=42.85 EndY=35.1046 EndZ=0
    g11: LineSegment StartX=42.85 StartY=35.1046 StartZ=0 EndX=42.85 EndY=38.3954 EndZ=0
    g12: LineSegment StartX=42.85 StartY=38.3954 StartZ=0 EndX=40 EndY=40.0409 EndZ=0
    g13: Circle [constr] CenterX=40 CenterY=36.75 CenterZ=0 NormalX=0 NormalY=0 NormalZ=1 AngleXU=0 Radius=3.2909
    g14: LineSegment StartX=72.85 StartY=38.3954 StartZ=0 EndX=70 EndY=40.0409 EndZ=0
    g15: LineSegment StartX=70 StartY=40.0409 StartZ=0 EndX=67.15 EndY=38.3954 EndZ=0
    g16: LineSegment StartX=67.15 StartY=38.3954 StartZ=0 EndX=67.15 EndY=35.1046 EndZ=0
    g17: LineSegment StartX=67.15 StartY=35.1046 StartZ=0 EndX=70 EndY=33.4591 EndZ=0
    g18: LineSegment StartX=70 StartY=33.4591 StartZ=0 EndX=72.85 EndY=35.1046 EndZ=0
    g19: LineSegment StartX=72.85 StartY=35.1046 StartZ=0 EndX=72.85 EndY=38.3954 EndZ=0
    g20: Circle [constr] CenterX=70 CenterY=36.75 CenterZ=0 NormalX=0 NormalY=0 NormalZ=1 AngleXU=0 Radius=3.2909
    g21: LineSegment StartX=106.75 StartY=26.5409 StartZ=0 EndX=103.9 EndY=24.8954 EndZ=0
    g22: LineSegment StartX=103.9 StartY=24.8954 StartZ=0 EndX=103.9 EndY=21.6046 EndZ=0
    g23: LineSegment StartX=103.9 StartY=21.6046 StartZ=0 EndX=106.75 EndY=19.9591 EndZ=0
    g24: LineSegment StartX=106.75 StartY=19.9591 StartZ=0 EndX=109.6 EndY=21.6046 EndZ=0
    g25: LineSegment StartX=109.6 StartY=21.6046 StartZ=0 EndX=109.6 EndY=24.8954 EndZ=0
    g26: LineSegment StartX=109.6 StartY=24.8954 StartZ=0 EndX=106.75 EndY=26.5409 EndZ=0
    g27: Circle [constr] CenterX=106.75 CenterY=23.25 CenterZ=0 NormalX=0 NormalY=0 NormalZ=1 AngleXU=0 Radius=3.2909
  constraints (68):
    c: Coincident(g0,g1)
    c: Coincident(g1,g2)
    c: Coincident(g2,g3)
    c: Coincident(g3,g4)
    c: Coincident(g4,g5)
    c: Coincident(g5,g0)
    c: Equal(g0, g1-g5) x5
    c: PointOnObject(g0,g6)
    c: PointOnObject(g1,g6)
    c: PointOnObject(g2,g6)
    c: PointOnObject(g3,g6)
    c: PointOnObject(g4,g6)
    c: PointOnObject(g5,g6)
    c: Coincident(g7,g8)
    c: Coincident(g8,g9)
    c: Coincident(g9,g10)
    c: Coincident(g10,g11)
    c: Coincident(g11,g12)
    c: Coincident(g12,g7)
    c: Equal(g7, g8-g12) x5
    c: PointOnObject(g7,g13)
    c: PointOnObject(g8,g13)
    c: PointOnObject(g9,g13)
    c: PointOnObject(g10,g13)
    c: PointOnObject(g11,g13)
    c: PointOnObject(g12,g13)
    c: Coincident(g14,g15)
    c: Coincident(g15,g16)
    c: Coincident(g16,g17)
    c: Coincident(g17,g18)
    c: Coincident(g18,g19)
    c: Coincident(g19,g14)
    c: Equal(g14, g15-g19) x5
    c: PointOnObject(g14,g20)
    c: PointOnObject(g15,g20)
    c: PointOnObject(g16,g20)
    c: PointOnObject(g17,g20)
    c: PointOnObject(g18,g20)
    c: PointOnObject(g19,g20)
    c: Coincident(g21,g22)
    c: Coincident(g22,g23)
    c: Coincident(g23,g24)
    c: Coincident(g24,g25)
    c: Coincident(g25,g26)
    c: Coincident(g26,g21)
    c: Equal(g21, g22-g26) x5
    c: PointOnObject(g21,g27)
    c: PointOnObject(g22,g27)
    c: PointOnObject(g23,g27)
    c: PointOnObject(g24,g27)
    c: PointOnObject(g25,g27)
    c: PointOnObject(g26,g27)
    c: Equal(g6,g13)
    c: Equal(g13,g20)
    c: Equal(g20,g27)
    c: Vertical(g22)
    c: Vertical(g19)
    c: Vertical(g11)
    c: Vertical(g4)
    c: Horizontal(g27,g6)
    c: Horizontal(g13,g20)
    c: DistanceX(g13,g20) = 30
    c: DistanceX(g6,g27) = 103.5
    c: DistanceX(g-1,g6) = 3.25
    c: DistanceY(g-1,g6) = 23.25
    c: DistanceY(g-1,g13) = 36.75
    c: DistanceX(g-1,g13) = 40
    c: DistanceX(g0,g4) = 5.7
FEATURE [PartDesign::Pocket] Pocket937  label="Nutholes Connection002"
  BaseFeature = -> Pocket934
  Length = 2.5
  Length2 = 100
  Profile = -> Sketch2677
  Type = 0
FEATURE [Sketcher::SketchObject] Sketch2678
  MapMode = 5
  Placement = pos=(112,0,0) rot=(0.57735,0.57735,0.57735;2.0944rad)
  Support = -> [Pocket937]
  sketch-geometry (4):
    g0: LineSegment StartX=-23.75 StartY=42 StartZ=0 EndX=108.85 EndY=42 EndZ=0
    g1: LineSegment StartX=108.85 StartY=42 StartZ=0 EndX=108.85 EndY=0 EndZ=0
    g2: LineSegment StartX=108.85 StartY=0 StartZ=0 EndX=-23.75 EndY=0 EndZ=0
    g3: LineSegment StartX=-23.75 StartY=0 StartZ=0 EndX=-23.75 EndY=42 EndZ=0
  constraints (12):
    c: Coincident(g0,g1)
    c: Coincident(g1,g2)
    c: Coincident(g2,g3)
    c: Coincident(g3,g0)
    c: Horizontal(g0)
    c: Horizontal(g2)
    c: Vertical(g1)
    c: Vertical(g3)
    c: PointOnObject(g2,g-1)
    c: DistanceY(g3,g3) = 42
    c: DistanceX(g-1,g1) = 108.85
    c: DistanceX(g2,g-1) = 23.75
FEATURE [PartDesign::Pocket] Pocket939  label="Remove Front"
  BaseFeature = -> Pocket937
  Length = 114
  Length2 = 100
  Profile = -> Sketch2678
  Type = 0
FEATURE [PartDesign::Body] Body800  label="Top_Cover_Split_Rear"
  Group = -> [Sketch2679,Pad1199,Thickness002,Pad1200,Pad1204,Sketch2675,Pocket936,Sketch2681,Pocket941,Sketch2670,Pocket938,Fillet275,Fillet273,Sketch2676,Pad1202,Fillet276,Fillet274,Sketch2672,Pocket940,Sketch2680,Pocket934,Sketch2677,Pocket937,Sketch2678,Pocket939]
  Origin = -> Origin1145
  Placement = pos=(0,0,0) rot=(1,0,0;3.14159rad)
  Tip = -> Pocket939
FEATURE [PartDesign::Body] Body807  label="M3x161"
  Group = -> [Sketch2661,Pad1209,Sketch2658,Pad1210,Sketch2660,Pocket942,Chamfer614]
  Origin = -> Origin1146
  Placement = pos=(66.75,13.5,0) rot=(0,0,1;0rad)
  Tip = -> Chamfer614
FEATURE [PartDesign::Body] Body808  label="M3x162"
  Group = -> [Sketch2662,Pad1206,Sketch2659,Pad1207,Sketch2657,Pocket935,Chamfer607]
  Origin = -> Origin1143
  Tip = -> Chamfer607
FEATURE [Sketcher::SketchObject] Sketch2684
  MapMode = 5
  Support = -> [XY_Plane1147]
  sketch-geometry (1):
    g0: Circle CenterX=0 CenterY=0 CenterZ=0 NormalX=0 NormalY=0 NormalZ=1 AngleXU=0 Radius=2.75
  constraints (2):
    c: Coincident(g0,g-1)
    c: Radius(g0) = 2.75
FEATURE [PartDesign::Pad] Pad1211  label="M3x8 Head194"
  Length = 3
  Length2 = 100
  Profile = -> Sketch2684
  Type = 0
FEATURE [Sketcher::SketchObject] Sketch2685
  MapMode = 5
  Placement = pos=(0,0,3) rot=(0,0,1;0rad)
  Support = -> [Pad1211]
  sketch-geometry (1):
    g0: Circle CenterX=0 CenterY=0 CenterZ=0 NormalX=0 NormalY=0 NormalZ=1 AngleXU=0 Radius=1.5
  constraints (2):
    c: Coincident(g0,g-1)
    c: Radius(g0) = 1.5
FEATURE [PartDesign::Pad] Pad1198  label="M3x8 Thread191"
  BaseFeature = -> Pad1211
  Length = 8
  Length2 = 100
  Profile = -> Sketch2685
  Type = 0
FEATURE [Sketcher::SketchObject] Sketch2686
  MapMode = 5
  Support = -> [XY_Plane1141]
  sketch-geometry (1):
    g0: Circle CenterX=0 CenterY=0 CenterZ=0 NormalX=0 NormalY=0 NormalZ=1 AngleXU=0 Radius=2.75
  constraints (2):
    c: Coincident(g0,g-1)
    c: Radius(g0) = 2.75
FEATURE [PartDesign::Pad] Pad1208  label="M3x8 Head192"
  Length = 3
  Length2 = 100
  Profile = -> Sketch2686
  Type = 0
FEATURE [Sketcher::SketchObject] Sketch2673
  MapMode = 5
  Placement = pos=(0,0,3) rot=(0,0,1;0rad)
  Support = -> [Pad1208]
  sketch-geometry (1):
    g0: Circle CenterX=0 CenterY=0 CenterZ=0 NormalX=0 NormalY=0 NormalZ=1 AngleXU=0 Radius=1.5
  constraints (2):
    c: Coincident(g0,g-1)
    c: Radius(g0) = 1.5
FEATURE [PartDesign::Pad] Pad1201  label="M3x8 Thread192"
  BaseFeature = -> Pad1208
  Length = 8
  Length2 = 100
  Profile = -> Sketch2673
  Type = 0
FEATURE [Sketcher::SketchObject] Sketch2669
  MapMode = 5
  Placement = pos=(0,0,0) rot=(1,0,0;3.14159rad)
  Support = -> [Pad1201]
  sketch-geometry (7):
    g0: LineSegment StartX=1.275 StartY=0.736122 StartZ=0 EndX=0 EndY=1.47224 EndZ=0
    g1: LineSegment StartX=0 StartY=1.47224 StartZ=0 EndX=-1.275 EndY=0.736122 EndZ=0
    g2: LineSegment StartX=-1.275 StartY=0.736122 StartZ=0 EndX=-1.275 EndY=-0.736122 EndZ=0
    g3: LineSegment StartX=-1.275 StartY=-0.736122 StartZ=0 EndX=1.34766e-11 EndY=-1.47224 EndZ=0
    g4: LineSegment StartX=1.34766e-11 StartY=-1.47224 StartZ=0 EndX=1.275 EndY=-0.736122 EndZ=0
    g5: LineSegment StartX=1.275 StartY=-0.736122 StartZ=0 EndX=1.275 EndY=0.736122 EndZ=0
    g6: Circle [constr] CenterX=0 CenterY=0 CenterZ=0 NormalX=0 NormalY=0 NormalZ=1 AngleXU=0 Radius=1.47224
  constraints (16):
    c: Coincident(g0,g1)
    c: Coincident(g1,g2)
    c: Coincident(g2,g3)
    c: Coincident(g3,g4)
    c: Coincident(g4,g5)
    c: Coincident(g5,g0)
    c: Equal(g0, g1-g5) x5
    c: PointOnObject(g0,g6)
    c: PointOnObject(g1,g6)
    c: PointOnObject(g2,g6)
    c: PointOnObject(g3,g6)
    c: PointOnObject(g4,g6)
    c: PointOnObject(g5,g6)
    c: Coincident(g6,g-1)
    c: PointOnObject(g0,g-2)
    c: DistanceX(g1,g0) = 2.55
FEATURE [PartDesign::Pocket] Pocket943  label="M3x8 Wrench193"
  BaseFeature = -> Pad1201
  Length = 1.3
  Length2 = 100
  Profile = -> Sketch2669
  Type = 0
FEATURE [PartDesign::Chamfer] Chamfer608  label="M3x8 Smooth191"
  Base = -> Pocket943 [Face11,Edge2,Edge24,Edge3]
  BaseFeature = -> Pocket943
  Size = 0.2
FEATURE [PartDesign::Body] Body804  label="M3x159"
  Group = -> [Sketch2686,Pad1208,Sketch2673,Pad1201,Sketch2669,Pocket943,Chamfer608]
  Origin = -> Origin1144
  Placement = pos=(36.75,13.5,0) rot=(0,0,1;0rad)
  Tip = -> Chamfer608
FEATURE [Sketcher::SketchObject] Sketch2687
  MapMode = 5
  Placement = pos=(0,0,0) rot=(1,0,0;3.14159rad)
  Support = -> [Pad1198]
  sketch-geometry (7):
    g0: LineSegment StartX=1.275 StartY=0.736122 StartZ=0 EndX=0 EndY=1.47224 EndZ=0
    g1: LineSegment StartX=0 StartY=1.47224 StartZ=0 EndX=-1.275 EndY=0.736122 EndZ=0
    g2: LineSegment StartX=-1.275 StartY=0.736122 StartZ=0 EndX=-1.275 EndY=-0.736122 EndZ=0
    g3: LineSegment StartX=-1.275 StartY=-0.736122 StartZ=0 EndX=1.34766e-11 EndY=-1.47224 EndZ=0
    g4: LineSegment StartX=1.34766e-11 StartY=-1.47224 StartZ=0 EndX=1.275 EndY=-0.736122 EndZ=0
    g5: LineSegment StartX=1.275 StartY=-0.736122 StartZ=0 EndX=1.275 EndY=0.736122 EndZ=0
    g6: Circle [constr] CenterX=0 CenterY=0 CenterZ=0 NormalX=0 NormalY=0 NormalZ=1 AngleXU=0 Radius=1.47224
  constraints (16):
    c: Coincident(g0,g1)
    c: Coincident(g1,g2)
    c: Coincident(g2,g3)
    c: Coincident(g3,g4)
    c: Coincident(g4,g5)
    c: Coincident(g5,g0)
    c: Equal(g0, g1-g5) x5
    c: PointOnObject(g0,g6)
    c: PointOnObject(g1,g6)
    c: PointOnObject(g2,g6)
    c: PointOnObject(g3,g6)
    c: PointOnObject(g4,g6)
    c: PointOnObject(g5,g6)
    c: Coincident(g6,g-1)
    c: PointOnObject(g0,g-2)
    c: DistanceX(g1,g0) = 2.55
FEATURE [PartDesign::Pocket] Pocket944  label="M3x8 Wrench194"
  BaseFeature = -> Pad1198
  Length = 1.3
  Length2 = 100
  Profile = -> Sketch2687
  Type = 0
FEATURE [PartDesign::Chamfer] Chamfer613  label="M3x8 Smooth192"
  Base = -> Pocket944 [Face11,Edge2,Edge24,Edge3]
  BaseFeature = -> Pocket944
  Size = 0.2
FEATURE [PartDesign::Body] Body806  label="M3x160"
  Group = -> [Sketch2684,Pad1211,Sketch2685,Pad1198,Sketch2687,Pocket944,Chamfer613]
  Origin = -> Origin1147
  Placement = pos=(103.5,0,0) rot=(0,0,1;0rad)
  Tip = -> Chamfer613
FEATURE [App::Part] Part316  label="Screws"
  Group = -> [Body808,Body804,Body807,Body806]
  Origin = -> Origin1142
  Placement = pos=(3.25,-114.5,-23.25) rot=(1,0,0;4.71239rad)
FEATURE [Sketcher::SketchObject] Sketch2689
  MapMode = 5
  Placement = pos=(0,-9.2e-15,42) rot=(0,0,1;0rad)
  Support = -> [Pad1194]
  sketch-geometry (16):
    g0: LineSegment StartX=-2 StartY=0 StartZ=0 EndX=30 EndY=0 EndZ=0
    g1: LineSegment StartX=30 StartY=0 StartZ=0 EndX=30 EndY=-23.75 EndZ=0
    g2: LineSegment StartX=30 StartY=-23.75 StartZ=0 EndX=-2 EndY=-23.75 EndZ=0
    g3: LineSegment StartX=-2 StartY=-23.75 StartZ=0 EndX=-2 EndY=0 EndZ=0
    g4: LineSegment StartX=112 StartY=0 StartZ=0 EndX=80 EndY=0 EndZ=0
    g5: LineSegment StartX=80 StartY=0 StartZ=0 EndX=80 EndY=-23.75 EndZ=0
    g6: LineSegment StartX=80 StartY=-23.75 StartZ=0 EndX=112 EndY=-23.75 EndZ=0
    g7: LineSegment StartX=112 StartY=-23.75 StartZ=0 EndX=112 EndY=0 EndZ=0
    g8: LineSegment StartX=-2 StartY=160 StartZ=0 EndX=30 EndY=160 EndZ=0
    g9: LineSegment StartX=30 StartY=160 StartZ=0 EndX=30 EndY=183.75 EndZ=0
    g10: LineSegment StartX=30 StartY=183.75 StartZ=0 EndX=-2 EndY=183.75 EndZ=0
    g11: LineSegment StartX=-2 StartY=183.75 StartZ=0 EndX=-2 EndY=160 EndZ=0
    g12: LineSegment StartX=112 StartY=183.75 StartZ=0 EndX=80 EndY=183.75 EndZ=0
    g13: LineSegment StartX=80 StartY=183.75 StartZ=0 EndX=80 EndY=160 EndZ=0
    g14: LineSegment StartX=80 StartY=160 StartZ=0 EndX=112 EndY=160 EndZ=0
    g15: LineSegment StartX=112 StartY=160 StartZ=0 EndX=112 EndY=183.75 EndZ=0
  constraints (48):
    c: Coincident(g0,g1)
    c: Coincident(g1,g2)
    c: Coincident(g2,g3)
    c: Coincident(g3,g0)
    c: Horizontal(g0)
    c: Horizontal(g2)
    c: Vertical(g1)
    c: Vertical(g3)
    c: PointOnObject(g0,g-1)
    c: Coincident(g4,g5)
    c: Coincident(g5,g6)
    c: Coincident(g6,g7)
    c: Coincident(g7,g4)
    c: Horizontal(g4)
    c: Horizontal(g6)
    c: Vertical(g5)
    c: Vertical(g7)
    c: Coincident(g8,g9)
    c: Coincident(g9,g10)
    c: Coincident(g10,g11)
    c: Coincident(g11,g8)
    c: Horizontal(g8)
    c: Horizontal(g10)
    c: Vertical(g9)
    c: Vertical(g11)
    c: Coincident(g12,g13)
    c: Coincident(g13,g14)
    c: Coincident(g14,g15)
    c: Coincident(g15,g12)
    c: Horizontal(g12)
    c: Horizontal(g14)
    c: Vertical(g13)
    c: Vertical(g15)
    c: Horizontal(g9,g12)
    c: Equal(g9,g13)
    c: Equal(g10,g12)
    c: Equal(g0,g8)
    c: Equal(g4,g14)
    c: Horizontal(g0,g4)
    c: Equal(g5,g1)
    c: DistanceX(g0,g4) = 50
    c: DistanceX(g0,g0) = 32
    c: DistanceY(g3,g3) = 23.75
    c: DistanceX(g0,g-1) = 2
    c: Vertical(g0,g8)
    c: Vertical(g13,g4)
    c: DistanceY(g0,g8) = 160
    c: Equal(g9,g1)
FEATURE [PartDesign::Pocket] Pocket931  label="Shoulders001"
  BaseFeature = -> Pad1194
  Length = 42
  Length2 = 100
  Profile = -> Sketch2689
  Type = 0
FEATURE [Sketcher::SketchObject] Sketch2653
  MapMode = 5
  Placement = pos=(112,0,0) rot=(0.57735,0.57735,0.57735;2.0944rad)
  Support = -> [Pocket931]
  sketch-geometry (6):
    g0: LineSegment StartX=0 StartY=-5 StartZ=0 EndX=-2e-16 EndY=12 EndZ=0
    g1: LineSegment StartX=-2e-16 StartY=12 StartZ=0 EndX=75 EndY=12 EndZ=0
    g2: LineSegment StartX=75 StartY=12 StartZ=0 EndX=105 EndY=0 EndZ=0
    g3: LineSegment StartX=105 StartY=0 StartZ=0 EndX=160 EndY=0 EndZ=0
    g4: LineSegment StartX=160 StartY=0 StartZ=0 EndX=160 EndY=-5 EndZ=0
    g5: LineSegment StartX=160 StartY=-5 StartZ=0 EndX=0 EndY=-5 EndZ=0
  constraints (18):
    c: PointOnObject(g0,g-2)
    c: Coincident(g0,g1)
    c: Horizontal(g1)
    c: Coincident(g1,g2)
    c: PointOnObject(g2,g-1)
    c: Coincident(g2,g3)
    c: Horizontal(g3)
    c: Coincident(g3,g4)
    c: Vertical(g4)
    c: Coincident(g4,g5)
    c: PointOnObject(g5,g-2)
    c: Horizontal(g5)
    c: Coincident(g0,g5)
    c: DistanceX(g1,g2) = 30
    c: DistanceX(g5,g5) = 160
    c: DistanceX(g1,g1) = 75
    c: DistanceY(g-1,g0) = 12
    c: DistanceY(g4,g4) = 5
FEATURE [PartDesign::Pocket] Pocket929  label="Side Detailing001"
  BaseFeature = -> Pocket931
  Length = 114
  Length2 = 100
  Profile = -> Sketch2653
  Type = 0
FEATURE [Sketcher::SketchObject] Sketch2682
  MapMode = 5
  Placement = pos=(0,-9.2e-15,42) rot=(0,0,1;0rad)
  Support = -> [Pocket929]
  sketch-geometry (4):
    g0: Circle CenterX=40 CenterY=-18.75 CenterZ=0 NormalX=0 NormalY=0 NormalZ=1 AngleXU=0 Radius=1.6
    g1: Circle CenterX=70 CenterY=-18.75 CenterZ=0 NormalX=0 NormalY=0 NormalZ=1 AngleXU=0 Radius=1.6
    g2: Circle CenterX=40 CenterY=178.75 CenterZ=0 NormalX=0 NormalY=0 NormalZ=1 AngleXU=0 Radius=1.6
    g3: Circle CenterX=70 CenterY=178.75 CenterZ=0 NormalX=0 NormalY=0 NormalZ=1 AngleXU=0 Radius=1.6
  constraints (12):
    c: DistanceX(g2,g3) = 30
    c: Equal(g2,g3)
    c: Equal(g3,g0)
    c: Equal(g0,g1)
    c: Horizontal(g2,g3)
    c: Horizontal(g0,g1)
    c: Vertical(g1,g3)
    c: Vertical(g0,g2)
    c: DistanceY(g0,g-1) = 18.75
    c: DistanceX(g-1,g0) = 40
    c: DistanceY(g-1,g2) = 178.75
    c: Radius(g3) = 1.6
FEATURE [PartDesign::Pocket] Pocket930  label="Screwholes012"
  BaseFeature = -> Pocket929
  Length = 2
  Length2 = 100
  Profile = -> Sketch2682
  Type = 0
FEATURE [App::Part] Part319  label="Nuts004"
  Group = -> [Body803,Body801,Body802,Body805]
  Origin = -> Origin1141
  Placement = pos=(3.25,-104.75,-23.25) rot=(1,0,0;4.71239rad)
FEATURE [App::Part] Part318  label="Nuts and Screws"
  Group = -> [Part319,Part316]
  Origin = -> Origin1139
FEATURE [PartDesign::Fillet] Fillet277  label="Round Corners001"
  Base = -> Pocket930 [Edge35,Edge66,Edge48,Edge12,Edge18,Edge44,Edge25,Edge76,Edge57,Edge60,Edge45,Edge9]
  BaseFeature = -> Pocket930
  Radius = 5
FEATURE [PartDesign::Fillet] Fillet278  label="Round Side Details001"
  Base = -> Fillet277 [Edge21,Edge29,Edge131,Edge132]
  BaseFeature = -> Fillet277
  Radius = 20
FEATURE [PartDesign::Pad] Pad1192  label="Screwpads001"
  BaseFeature = -> Fillet278
  Length = 5.5
  Length2 = 5.5
  Profile = -> Sketch2656
  Type = 4
FEATURE [PartDesign::Fillet] Fillet280  label="Smooth Screwpad Edges001"
  Base = -> Pad1192 [Edge35,Edge33,Edge137,Edge141,Edge145,Edge149,Edge182,Edge77,Edge73,Edge71,Edge75,Edge123]
  BaseFeature = -> Pad1192
  Radius = 1
FEATURE [PartDesign::Fillet] Fillet279  label="Smooth Screwpad Edges Side Details001"
  Base = -> Fillet280 [Edge23,Edge202]
  BaseFeature = -> Fillet280
  Radius = 0.2
FEATURE [Sketcher::SketchObject] Sketch2654
  MapMode = 5
  Placement = pos=(-8.12e-14,114.35,8.35e-14) rot=(0,0.707107,0.707107;3.14159rad)
  Support = -> [Fillet279]
  sketch-geometry (4):
    g0: Circle CenterX=-106.75 CenterY=23.25 CenterZ=0 NormalX=0 NormalY=0 NormalZ=1 AngleXU=0 Radius=1.6
    g1: Circle CenterX=-70 CenterY=36.75 CenterZ=0 NormalX=0 NormalY=0 NormalZ=1 AngleXU=0 Radius=1.6
    g2: Circle CenterX=-40 CenterY=36.75 CenterZ=0 NormalX=0 NormalY=0 NormalZ=1 AngleXU=0 Radius=1.6
    g3: Circle CenterX=-3.25 CenterY=23.25 CenterZ=0 NormalX=0 NormalY=0 NormalZ=1 AngleXU=0 Radius=1.6
  constraints (12):
    c: Equal(g0,g1)
    c: Equal(g1,g2)
    c: Equal(g2,g3)
    c: DistanceX(g1,g2) = 30
    c: DistanceX(g3,g-1) = 3.25
    c: DistanceY(g-1,g3) = 23.25
    c: DistanceX(g0,g3) = 103.5
    c: Horizontal(g3,g0)
    c: Horizontal(g1,g2)
    c: DistanceX(g2,g-1) = 40
    c: DistanceY(g-1,g2) = 36.75
    c: Radius(g3) = 1.6
FEATURE [PartDesign::Pocket] Pocket932  label="Screwholes Connection001"
  BaseFeature = -> Fillet279
  Length = 11
  Length2 = 100
  Profile = -> Sketch2654
  Type = 0
FEATURE [Sketcher::SketchObject] Sketch2683
  MapMode = 5
  Placement = pos=(-8.12e-14,114.35,8.35e-14) rot=(0,0.707107,0.707107;3.14159rad)
  Support = -> [Pocket932]
  sketch-geometry (4):
    g0: Circle CenterX=-106.75 CenterY=23.25 CenterZ=0 NormalX=0 NormalY=0 NormalZ=1 AngleXU=0 Radius=2.85
    g1: Circle CenterX=-70 CenterY=36.75 CenterZ=0 NormalX=0 NormalY=0 NormalZ=1 AngleXU=0 Radius=2.85
    g2: Circle CenterX=-40 CenterY=36.75 CenterZ=0 NormalX=0 NormalY=0 NormalZ=1 AngleXU=0 Radius=2.85
    g3: Circle CenterX=-3.25 CenterY=23.25 CenterZ=0 NormalX=0 NormalY=0 NormalZ=1 AngleXU=0 Radius=2.85
  constraints (12):
    c: Equal(g0,g1)
    c: Equal(g1,g2)
    c: Equal(g2,g3)
    c: Radius(g3) = 2.85
    c: DistanceX(g3,g-1) = 3.25
    c: Horizontal(g3,g0)
    c: Horizontal(g1,g2)
    c: DistanceX(g0,g3) = 103.5
    c: DistanceX(g1,g2) = 30
    c: DistanceY(g-1,g2) = 36.75
    c: DistanceX(g2,g-1) = 40
    c: DistanceY(g-1,g3) = 23.25
FEATURE [PartDesign::Pocket] Pocket928  label="Screwheads Connection001"
  BaseFeature = -> Pocket932
  Length = 3
  Length2 = 100
  Profile = -> Sketch2683
  Type = 0
FEATURE [Sketcher::SketchObject] Sketch2655
  MapMode = 5
  Placement = pos=(7.34e-14,103.35,7.54e-14) rot=(1,0,0;1.5708rad)
  Support = -> [Pocket928]
  sketch-geometry (28):
    g0: LineSegment StartX=3.25 StartY=26.5409 StartZ=0 EndX=0.4 EndY=24.8954 EndZ=0
    g1: LineSegment StartX=0.4 StartY=24.8954 StartZ=0 EndX=0.4 EndY=21.6046 EndZ=0
    g2: LineSegment StartX=0.4 StartY=21.6046 StartZ=0 EndX=3.25 EndY=19.9591 EndZ=0
    g3: LineSegment StartX=3.25 StartY=19.9591 StartZ=0 EndX=6.1 EndY=21.6046 EndZ=0
    g4: LineSegment StartX=6.1 StartY=21.6046 StartZ=0 EndX=6.1 EndY=24.8954 EndZ=0
    g5: LineSegment StartX=6.1 StartY=24.8954 StartZ=0 EndX=3.25 EndY=26.5409 EndZ=0
    g6: Circle [constr] CenterX=3.25 CenterY=23.25 CenterZ=0 NormalX=0 NormalY=0 NormalZ=1 AngleXU=0 Radius=3.2909
    g7: LineSegment StartX=40 StartY=40.0409 StartZ=0 EndX=37.15 EndY=38.3954 EndZ=0
    g8: LineSegment StartX=37.15 StartY=38.3954 StartZ=0 EndX=37.15 EndY=35.1046 EndZ=0
    g9: LineSegment StartX=37.15 StartY=35.1046 StartZ=0 EndX=40 EndY=33.4591 EndZ=0
    g10: LineSegment StartX=40 StartY=33.4591 StartZ=0 EndX=42.85 EndY=35.1046 EndZ=0
    g11: LineSegment StartX=42.85 StartY=35.1046 StartZ=0 EndX=42.85 EndY=38.3954 EndZ=0
    g12: LineSegment StartX=42.85 StartY=38.3954 StartZ=0 EndX=40 EndY=40.0409 EndZ=0
    g13: Circle [constr] CenterX=40 CenterY=36.75 CenterZ=0 NormalX=0 NormalY=0 NormalZ=1 AngleXU=0 Radius=3.2909
    g14: LineSegment StartX=72.85 StartY=38.3954 StartZ=0 EndX=70 EndY=40.0409 EndZ=0
    g15: LineSegment StartX=70 StartY=40.0409 StartZ=0 EndX=67.15 EndY=38.3954 EndZ=0
    g16: LineSegment StartX=67.15 StartY=38.3954 StartZ=0 EndX=67.15 EndY=35.1046 EndZ=0
    g17: LineSegment StartX=67.15 StartY=35.1046 StartZ=0 EndX=70 EndY=33.4591 EndZ=0
    g18: LineSegment StartX=70 StartY=33.4591 StartZ=0 EndX=72.85 EndY=35.1046 EndZ=0
    g19: LineSegment StartX=72.85 StartY=35.1046 StartZ=0 EndX=72.85 EndY=38.3954 EndZ=0
    g20: Circle [constr] CenterX=70 CenterY=36.75 CenterZ=0 NormalX=0 NormalY=0 NormalZ=1 AngleXU=0 Radius=3.2909
    g21: LineSegment StartX=106.75 StartY=26.5409 StartZ=0 EndX=103.9 EndY=24.8954 EndZ=0
    g22: LineSegment StartX=103.9 StartY=24.8954 StartZ=0 EndX=103.9 EndY=21.6046 EndZ=0
    g23: LineSegment StartX=103.9 StartY=21.6046 StartZ=0 EndX=106.75 EndY=19.9591 EndZ=0
    g24: LineSegment StartX=106.75 StartY=19.9591 StartZ=0 EndX=109.6 EndY=21.6046 EndZ=0
    g25: LineSegment StartX=109.6 StartY=21.6046 StartZ=0 EndX=109.6 EndY=24.8954 EndZ=0
    g26: LineSegment StartX=109.6 StartY=24.8954 StartZ=0 EndX=106.75 EndY=26.5409 EndZ=0
    g27: Circle [constr] CenterX=106.75 CenterY=23.25 CenterZ=0 NormalX=0 NormalY=0 NormalZ=1 AngleXU=0 Radius=3.2909
  constraints (68):
    c: Coincident(g0,g1)
    c: Coincident(g1,g2)
    c: Coincident(g2,g3)
    c: Coincident(g3,g4)
    c: Coincident(g4,g5)
    c: Coincident(g5,g0)
    c: Equal(g0, g1-g5) x5
    c: PointOnObject(g0,g6)
    c: PointOnObject(g1,g6)
    c: PointOnObject(g2,g6)
    c: PointOnObject(g3,g6)
    c: PointOnObject(g4,g6)
    c: PointOnObject(g5,g6)
    c: Coincident(g7,g8)
    c: Coincident(g8,g9)
    c: Coincident(g9,g10)
    c: Coincident(g10,g11)
    c: Coincident(g11,g12)
    c: Coincident(g12,g7)
    c: Equal(g7, g8-g12) x5
    c: PointOnObject(g7,g13)
    c: PointOnObject(g8,g13)
    c: PointOnObject(g9,g13)
    c: PointOnObject(g10,g13)
    c: PointOnObject(g11,g13)
    c: PointOnObject(g12,g13)
    c: Coincident(g14,g15)
    c: Coincident(g15,g16)
    c: Coincident(g16,g17)
    c: Coincident(g17,g18)
    c: Coincident(g18,g19)
    c: Coincident(g19,g14)
    c: Equal(g14, g15-g19) x5
    c: PointOnObject(g14,g20)
    c: PointOnObject(g15,g20)
    c: PointOnObject(g16,g20)
    c: PointOnObject(g17,g20)
    c: PointOnObject(g18,g20)
    c: PointOnObject(g19,g20)
    c: Coincident(g21,g22)
    c: Coincident(g22,g23)
    c: Coincident(g23,g24)
    c: Coincident(g24,g25)
    c: Coincident(g25,g26)
    c: Coincident(g26,g21)
    c: Equal(g21, g22-g26) x5
    c: PointOnObject(g21,g27)
    c: PointOnObject(g22,g27)
    c: PointOnObject(g23,g27)
    c: PointOnObject(g24,g27)
    c: PointOnObject(g25,g27)
    c: PointOnObject(g26,g27)
    c: Equal(g6,g13)
    c: Equal(g13,g20)
    c: Equal(g20,g27)
    c: Vertical(g22)
    c: Vertical(g19)
    c: Vertical(g11)
    c: Vertical(g4)
    c: Horizontal(g27,g6)
    c: Horizontal(g13,g20)
    c: DistanceX(g13,g20) = 30
    c: DistanceX(g6,g27) = 103.5
    c: DistanceX(g-1,g6) = 3.25
    c: DistanceY(g-1,g6) = 23.25
    c: DistanceY(g-1,g13) = 36.75
    c: DistanceX(g-1,g13) = 40
    c: DistanceX(g0,g4) = 5.7
FEATURE [PartDesign::Pocket] Pocket927  label="Nutholes Connection001"
  BaseFeature = -> Pocket928
  Length = 2.5
  Length2 = 100
  Profile = -> Sketch2655
  Type = 0
FEATURE [Sketcher::SketchObject] Sketch2688
  MapMode = 5
  Placement = pos=(112,0,0) rot=(0.57735,0.57735,0.57735;2.0944rad)
  Support = -> [Pocket927]
  sketch-geometry (4):
    g0: LineSegment StartX=188.85 StartY=42 StartZ=0 EndX=108.85 EndY=42 EndZ=0
    g1: LineSegment StartX=108.85 StartY=42 StartZ=0 EndX=108.85 EndY=0 EndZ=0
    g2: LineSegment StartX=108.85 StartY=0 StartZ=0 EndX=188.85 EndY=0 EndZ=0
    g3: LineSegment StartX=188.85 StartY=0 StartZ=0 EndX=188.85 EndY=42 EndZ=0
  constraints (12):
    c: Coincident(g0,g1)
    c: Coincident(g1,g2)
    c: Coincident(g2,g3)
    c: Coincident(g3,g0)
    c: Horizontal(g0)
    c: Horizontal(g2)
    c: Vertical(g1)
    c: Vertical(g3)
    c: PointOnObject(g2,g-1)
    c: DistanceY(g3,g3) = 42
    c: DistanceX(g-1,g1) = 108.85
    c: DistanceX(g2,g2) = 80
FEATURE [PartDesign::Pocket] Pocket933  label="Remove Rear"
  BaseFeature = -> Pocket927
  Length = 114
  Length2 = 100
  Profile = -> Sketch2688
  Type = 0
FEATURE [PartDesign::Body] Body809  label="Top_Cover_Split_Front"
  Group = -> [Sketch2652,Pad1193,Thickness003,Pad1195,Pad1194,Sketch2689,Pocket931,Sketch2653,Pocket929,Sketch2682,Pocket930,Fillet277,Fillet278,Sketch2656,Pad1192,Fillet280,Fillet279,Sketch2654,Pocket932,Sketch2683,Pocket928,Sketch2655,Pocket927,Sketch2688,Pocket933]
  Origin = -> Origin1150
  Placement = pos=(0,0,0) rot=(1,0,0;3.14159rad)
  Tip = -> Pocket933
FEATURE [App::Part] Part317  label="Top Cover Assembly"
  Group = -> [Body809,Body800,Part318]
  Origin = -> Origin1149
  Placement = pos=(-28,-154.75,196.75) rot=(0.707107,0.707107,0;3.14159rad)
FEATURE [Sketcher::SketchObject] Sketch2692
  MapMode = 5
  Support = -> [XY_Plane1151]
  sketch-geometry (1):
    g0: Circle CenterX=0 CenterY=0 CenterZ=0 NormalX=0 NormalY=0 NormalZ=1 AngleXU=0 Radius=2.75
  constraints (2):
    c: Coincident(g0,g-1)
    c: Radius(g0) = 2.75
FEATURE [Sketcher::SketchObject] Sketch2693
  MapMode = 5
  Support = -> [XY_Plane1149]
  sketch-geometry (1):
    g0: Circle CenterX=0 CenterY=0 CenterZ=0 NormalX=0 NormalY=0 NormalZ=1 AngleXU=0 Radius=2.75
  constraints (2):
    c: Coincident(g0,g-1)
    c: Radius(g0) = 2.75
FEATURE [PartDesign::Pad] Pad1212  label="M3x8 Head195"
  Length = 3
  Length2 = 100
  Profile = -> Sketch2692
  Type = 0
FEATURE [PartDesign::Pad] Pad1216  label="M3x8 Head197"
  Length = 3
  Length2 = 100
  Profile = -> Sketch2693
  Type = 0
FEATURE [Sketcher::SketchObject] Sketch2690
  MapMode = 5
  Placement = pos=(0,0,3) rot=(0,0,1;0rad)
  Support = -> [Pad1216]
  sketch-geometry (1):
    g0: Circle CenterX=0 CenterY=0 CenterZ=0 NormalX=0 NormalY=0 NormalZ=1 AngleXU=0 Radius=1.5
  constraints (2):
    c: Coincident(g0,g-1)
    c: Radius(g0) = 1.5
FEATURE [PartDesign::Pad] Pad1215  label="M3x8 Thread196"
  BaseFeature = -> Pad1216
  Length = 8
  Length2 = 100
  Profile = -> Sketch2690
  Type = 0
FEATURE [Sketcher::SketchObject] Sketch2695
  MapMode = 5
  Support = -> [XY_Plane1150]
  sketch-geometry (1):
    g0: Circle CenterX=0 CenterY=0 CenterZ=0 NormalX=0 NormalY=0 NormalZ=1 AngleXU=0 Radius=2.75
  constraints (2):
    c: Coincident(g0,g-1)
    c: Radius(g0) = 2.75
FEATURE [PartDesign::Pad] Pad1218  label="M3x8 Head198"
  Length = 3
  Length2 = 100
  Profile = -> Sketch2695
  Type = 0
FEATURE [Sketcher::SketchObject] Sketch2694
  MapMode = 5
  Placement = pos=(0,0,3) rot=(0,0,1;0rad)
  Support = -> [Pad1218]
  sketch-geometry (1):
    g0: Circle CenterX=0 CenterY=0 CenterZ=0 NormalX=0 NormalY=0 NormalZ=1 AngleXU=0 Radius=1.5
  constraints (2):
    c: Coincident(g0,g-1)
    c: Radius(g0) = 1.5
FEATURE [PartDesign::Pad] Pad1217  label="M3x8 Thread197"
  BaseFeature = -> Pad1218
  Length = 8
  Length2 = 100
  Profile = -> Sketch2694
  Type = 0
FEATURE [Sketcher::SketchObject] Sketch2696
  MapMode = 5
  Placement = pos=(0,0,0) rot=(1,0,0;3.14159rad)
  Support = -> [Pad1215]
  sketch-geometry (7):
    g0: LineSegment StartX=1.275 StartY=0.736122 StartZ=0 EndX=0 EndY=1.47224 EndZ=0
    g1: LineSegment StartX=0 StartY=1.47224 StartZ=0 EndX=-1.275 EndY=0.736122 EndZ=0
    g2: LineSegment StartX=-1.275 StartY=0.736122 StartZ=0 EndX=-1.275 EndY=-0.736122 EndZ=0
    g3: LineSegment StartX=-1.275 StartY=-0.736122 StartZ=0 EndX=1.34766e-11 EndY=-1.47224 EndZ=0
    g4: LineSegment StartX=1.34766e-11 StartY=-1.47224 StartZ=0 EndX=1.275 EndY=-0.736122 EndZ=0
    g5: LineSegment StartX=1.275 StartY=-0.736122 StartZ=0 EndX=1.275 EndY=0.736122 EndZ=0
    g6: Circle [constr] CenterX=0 CenterY=0 CenterZ=0 NormalX=0 NormalY=0 NormalZ=1 AngleXU=0 Radius=1.47224
  constraints (16):
    c: Coincident(g0,g1)
    c: Coincident(g1,g2)
    c: Coincident(g2,g3)
    c: Coincident(g3,g4)
    c: Coincident(g4,g5)
    c: Coincident(g5,g0)
    c: Equal(g0, g1-g5) x5
    c: PointOnObject(g0,g6)
    c: PointOnObject(g1,g6)
    c: PointOnObject(g2,g6)
    c: PointOnObject(g3,g6)
    c: PointOnObject(g4,g6)
    c: PointOnObject(g5,g6)
    c: Coincident(g6,g-1)
    c: PointOnObject(g0,g-2)
    c: DistanceX(g1,g0) = 2.55
FEATURE [PartDesign::Pocket] Pocket945  label="M3x8 Wrench195"
  BaseFeature = -> Pad1215
  Length = 1.3
  Length2 = 100
  Profile = -> Sketch2696
  Type = 0
FEATURE [PartDesign::Chamfer] Chamfer615  label="M3x8 Smooth194"
  Base = -> Pocket945 [Face11,Edge2,Edge24,Edge3]
  BaseFeature = -> Pocket945
  Size = 0.2
FEATURE [PartDesign::Body] Body812  label="M3x165"
  Group = -> [Sketch2693,Pad1216,Sketch2690,Pad1215,Sketch2696,Pocket945,Chamfer615]
  Origin = -> Origin1154
  Placement = pos=(-9e-15,-10,76.2) rot=(0,1,0;3.14159rad)
  Tip = -> Chamfer615
FEATURE [Sketcher::SketchObject] Sketch2697
  MapMode = 5
  Placement = pos=(0,0,3) rot=(0,0,1;0rad)
  Support = -> [Pad1212]
  sketch-geometry (1):
    g0: Circle CenterX=0 CenterY=0 CenterZ=0 NormalX=0 NormalY=0 NormalZ=1 AngleXU=0 Radius=1.5
  constraints (2):
    c: Coincident(g0,g-1)
    c: Radius(g0) = 1.5
FEATURE [PartDesign::Pad] Pad1214  label="M3x8 Thread195"
  BaseFeature = -> Pad1212
  Length = 8
  Length2 = 100
  Profile = -> Sketch2697
  Type = 0
FEATURE [Sketcher::SketchObject] Sketch2691
  MapMode = 5
  Placement = pos=(0,0,0) rot=(1,0,0;3.14159rad)
  Support = -> [Pad1214]
  sketch-geometry (7):
    g0: LineSegment StartX=1.275 StartY=0.736122 StartZ=0 EndX=0 EndY=1.47224 EndZ=0
    g1: LineSegment StartX=0 StartY=1.47224 StartZ=0 EndX=-1.275 EndY=0.736122 EndZ=0
    g2: LineSegment StartX=-1.275 StartY=0.736122 StartZ=0 EndX=-1.275 EndY=-0.736122 EndZ=0
    g3: LineSegment StartX=-1.275 StartY=-0.736122 StartZ=0 EndX=1.34766e-11 EndY=-1.47224 EndZ=0
    g4: LineSegment StartX=1.34766e-11 StartY=-1.47224 StartZ=0 EndX=1.275 EndY=-0.736122 EndZ=0
    g5: LineSegment StartX=1.275 StartY=-0.736122 StartZ=0 EndX=1.275 EndY=0.736122 EndZ=0
    g6: Circle [constr] CenterX=0 CenterY=0 CenterZ=0 NormalX=0 NormalY=0 NormalZ=1 AngleXU=0 Radius=1.47224
  constraints (16):
    c: Coincident(g0,g1)
    c: Coincident(g1,g2)
    c: Coincident(g2,g3)
    c: Coincident(g3,g4)
    c: Coincident(g4,g5)
    c: Coincident(g5,g0)
    c: Equal(g0, g1-g5) x5
    c: PointOnObject(g0,g6)
    c: PointOnObject(g1,g6)
    c: PointOnObject(g2,g6)
    c: PointOnObject(g3,g6)
    c: PointOnObject(g4,g6)
    c: PointOnObject(g5,g6)
    c: Coincident(g6,g-1)
    c: PointOnObject(g0,g-2)
    c: DistanceX(g1,g0) = 2.55
FEATURE [PartDesign::Pocket] Pocket948  label="M3x8 Wrench198"
  BaseFeature = -> Pad1214
  Length = 1.3
  Length2 = 100
  Profile = -> Sketch2691
  Type = 0
FEATURE [PartDesign::Chamfer] Chamfer617  label="M3x8 Smooth196"
  Base = -> Pocket948 [Face11,Edge2,Edge24,Edge3]
  BaseFeature = -> Pocket948
  Size = 0.2
FEATURE [PartDesign::Body] Body811  label="M3x164"
  Group = -> [Sketch2692,Pad1212,Sketch2697,Pad1214,Sketch2691,Pocket948,Chamfer617]
  Origin = -> Origin1151
  Placement = pos=(0,0,-4.25) rot=(0,0,1;0rad)
  Tip = -> Chamfer617
FEATURE [Sketcher::SketchObject] Sketch2698
  MapMode = 5
  Placement = pos=(0,0,0) rot=(1,0,0;3.14159rad)
  Support = -> [Pad1217]
  sketch-geometry (7):
    g0: LineSegment StartX=1.275 StartY=0.736122 StartZ=0 EndX=0 EndY=1.47224 EndZ=0
    g1: LineSegment StartX=0 StartY=1.47224 StartZ=0 EndX=-1.275 EndY=0.736122 EndZ=0
    g2: LineSegment StartX=-1.275 StartY=0.736122 StartZ=0 EndX=-1.275 EndY=-0.736122 EndZ=0
    g3: LineSegment StartX=-1.275 StartY=-0.736122 StartZ=0 EndX=1.34766e-11 EndY=-1.47224 EndZ=0
    g4: LineSegment StartX=1.34766e-11 StartY=-1.47224 StartZ=0 EndX=1.275 EndY=-0.736122 EndZ=0
    g5: LineSegment StartX=1.275 StartY=-0.736122 StartZ=0 EndX=1.275 EndY=0.736122 EndZ=0
    g6: Circle [constr] CenterX=0 CenterY=0 CenterZ=0 NormalX=0 NormalY=0 NormalZ=1 AngleXU=0 Radius=1.47224
  constraints (16):
    c: Coincident(g0,g1)
    c: Coincident(g1,g2)
    c: Coincident(g2,g3)
    c: Coincident(g3,g4)
    c: Coincident(g4,g5)
    c: Coincident(g5,g0)
    c: Equal(g0, g1-g5) x5
    c: PointOnObject(g0,g6)
    c: PointOnObject(g1,g6)
    c: PointOnObject(g2,g6)
    c: PointOnObject(g3,g6)
    c: PointOnObject(g4,g6)
    c: PointOnObject(g5,g6)
    c: Coincident(g6,g-1)
    c: PointOnObject(g0,g-2)
    c: DistanceX(g1,g0) = 2.55
FEATURE [PartDesign::Pocket] Pocket946  label="M3x8 Wrench196"
  BaseFeature = -> Pad1217
  Length = 1.3
  Length2 = 100
  Profile = -> Sketch2698
  Type = 0
FEATURE [PartDesign::Chamfer] Chamfer616  label="M3x8 Smooth195"
  Base = -> Pocket946 [Face11,Edge2,Edge24,Edge3]
  BaseFeature = -> Pocket946
  Size = 0.2
FEATURE [PartDesign::Body] Body813  label="M3x166"
  Group = -> [Sketch2695,Pad1218,Sketch2694,Pad1217,Sketch2698,Pocket946,Chamfer616]
  Origin = -> Origin1155
  Placement = pos=(0,10,-4.25) rot=(0,0,1;0rad)
  Tip = -> Chamfer616
FEATURE [Sketcher::SketchObject] Sketch2701
  MapMode = 5
  Support = -> [XY_Plane1153]
  sketch-geometry (1):
    g0: Circle CenterX=0 CenterY=0 CenterZ=0 NormalX=0 NormalY=0 NormalZ=1 AngleXU=0 Radius=2.75
  constraints (2):
    c: Coincident(g0,g-1)
    c: Radius(g0) = 2.75
FEATURE [PartDesign::Pad] Pad1213  label="M3x8 Head196"
  Length = 3
  Length2 = 100
  Profile = -> Sketch2701
  Type = 0
FEATURE [Sketcher::SketchObject] Sketch2699
  MapMode = 5
  Placement = pos=(0,0,3) rot=(0,0,1;0rad)
  Support = -> [Pad1213]
  sketch-geometry (1):
    g0: Circle CenterX=0 CenterY=0 CenterZ=0 NormalX=0 NormalY=0 NormalZ=1 AngleXU=0 Radius=1.5
  constraints (2):
    c: Coincident(g0,g-1)
    c: Radius(g0) = 1.5
FEATURE [PartDesign::Pad] Pad1219  label="M3x8 Thread198"
  BaseFeature = -> Pad1213
  Length = 8
  Length2 = 100
  Profile = -> Sketch2699
  Type = 0
FEATURE [Sketcher::SketchObject] Sketch2700
  MapMode = 5
  Placement = pos=(0,0,0) rot=(1,0,0;3.14159rad)
  Support = -> [Pad1219]
  sketch-geometry (7):
    g0: LineSegment StartX=1.275 StartY=0.736122 StartZ=0 EndX=0 EndY=1.47224 EndZ=0
    g1: LineSegment StartX=0 StartY=1.47224 StartZ=0 EndX=-1.275 EndY=0.736122 EndZ=0
    g2: LineSegment StartX=-1.275 StartY=0.736122 StartZ=0 EndX=-1.275 EndY=-0.736122 EndZ=0
    g3: LineSegment StartX=-1.275 StartY=-0.736122 StartZ=0 EndX=1.34766e-11 EndY=-1.47224 EndZ=0
    g4: LineSegment StartX=1.34766e-11 StartY=-1.47224 StartZ=0 EndX=1.275 EndY=-0.736122 EndZ=0
    g5: LineSegment StartX=1.275 StartY=-0.736122 StartZ=0 EndX=1.275 EndY=0.736122 EndZ=0
    g6: Circle [constr] CenterX=0 CenterY=0 CenterZ=0 NormalX=0 NormalY=0 NormalZ=1 AngleXU=0 Radius=1.47224
  constraints (16):
    c: Coincident(g0,g1)
    c: Coincident(g1,g2)
    c: Coincident(g2,g3)
    c: Coincident(g3,g4)
    c: Coincident(g4,g5)
    c: Coincident(g5,g0)
    c: Equal(g0, g1-g5) x5
    c: PointOnObject(g0,g6)
    c: PointOnObject(g1,g6)
    c: PointOnObject(g2,g6)
    c: PointOnObject(g3,g6)
    c: PointOnObject(g4,g6)
    c: PointOnObject(g5,g6)
    c: Coincident(g6,g-1)
    c: PointOnObject(g0,g-2)
    c: DistanceX(g1,g0) = 2.55
FEATURE [PartDesign::Pocket] Pocket947  label="M3x8 Wrench197"
  BaseFeature = -> Pad1219
  Length = 1.3
  Length2 = 100
  Profile = -> Sketch2700
  Type = 0
FEATURE [PartDesign::Chamfer] Chamfer618  label="M3x8 Smooth197"
  Base = -> Pocket947 [Face11,Edge2,Edge24,Edge3]
  BaseFeature = -> Pocket947
  Size = 0.2
FEATURE [PartDesign::Body] Body810  label="M3x163"
  Group = -> [Sketch2701,Pad1213,Sketch2699,Pad1219,Sketch2700,Pocket947,Chamfer618]
  Origin = -> Origin1153
  Placement = pos=(-9e-15,20.05,76.2) rot=(0,1,0;3.14159rad)
  Tip = -> Chamfer618
FEATURE [App::Part] Part320  label="Top_Cover_Screws002"
  Group = -> [Body811,Body813,Body812,Body810]
  Origin = -> Origin1152
  Placement = pos=(-206.75,-104.5,165.6) rot=(0,0,1;0rad)
FEATURE [Sketcher::SketchObject] Sketch2704
  MapMode = 5
  Support = -> [XY_Plane1157]
  sketch-geometry (1):
    g0: Circle CenterX=0 CenterY=0 CenterZ=0 NormalX=0 NormalY=0 NormalZ=1 AngleXU=0 Radius=2.75
  constraints (2):
    c: Coincident(g0,g-1)
    c: Radius(g0) = 2.75
FEATURE [Sketcher::SketchObject] Sketch2705
  MapMode = 5
  Support = -> [XY_Plane1155]
  sketch-geometry (1):
    g0: Circle CenterX=0 CenterY=0 CenterZ=0 NormalX=0 NormalY=0 NormalZ=1 AngleXU=0 Radius=2.75
  constraints (2):
    c: Coincident(g0,g-1)
    c: Radius(g0) = 2.75
FEATURE [PartDesign::Pad] Pad1220  label="M3x8 Head199"
  Length = 3
  Length2 = 100
  Profile = -> Sketch2704
  Type = 0
FEATURE [PartDesign::Pad] Pad1224  label="M3x8 Head201"
  Length = 3
  Length2 = 100
  Profile = -> Sketch2705
  Type = 0
FEATURE [Sketcher::SketchObject] Sketch2702
  MapMode = 5
  Placement = pos=(0,0,3) rot=(0,0,1;0rad)
  Support = -> [Pad1224]
  sketch-geometry (1):
    g0: Circle CenterX=0 CenterY=0 CenterZ=0 NormalX=0 NormalY=0 NormalZ=1 AngleXU=0 Radius=1.5
  constraints (2):
    c: Coincident(g0,g-1)
    c: Radius(g0) = 1.5
FEATURE [PartDesign::Pad] Pad1223  label="M3x8 Thread200"
  BaseFeature = -> Pad1224
  Length = 8
  Length2 = 100
  Profile = -> Sketch2702
  Type = 0
FEATURE [Sketcher::SketchObject] Sketch2707
  MapMode = 5
  Support = -> [XY_Plane1156]
  sketch-geometry (1):
    g0: Circle CenterX=0 CenterY=0 CenterZ=0 NormalX=0 NormalY=0 NormalZ=1 AngleXU=0 Radius=2.75
  constraints (2):
    c: Coincident(g0,g-1)
    c: Radius(g0) = 2.75
FEATURE [PartDesign::Pad] Pad1226  label="M3x8 Head202"
  Length = 3
  Length2 = 100
  Profile = -> Sketch2707
  Type = 0
FEATURE [Sketcher::SketchObject] Sketch2706
  MapMode = 5
  Placement = pos=(0,0,3) rot=(0,0,1;0rad)
  Support = -> [Pad1226]
  sketch-geometry (1):
    g0: Circle CenterX=0 CenterY=0 CenterZ=0 NormalX=0 NormalY=0 NormalZ=1 AngleXU=0 Radius=1.5
  constraints (2):
    c: Coincident(g0,g-1)
    c: Radius(g0) = 1.5
FEATURE [PartDesign::Pad] Pad1225  label="M3x8 Thread201"
  BaseFeature = -> Pad1226
  Length = 8
  Length2 = 100
  Profile = -> Sketch2706
  Type = 0
FEATURE [Sketcher::SketchObject] Sketch2708
  MapMode = 5
  Placement = pos=(0,0,0) rot=(1,0,0;3.14159rad)
  Support = -> [Pad1223]
  sketch-geometry (7):
    g0: LineSegment StartX=1.275 StartY=0.736122 StartZ=0 EndX=0 EndY=1.47224 EndZ=0
    g1: LineSegment StartX=0 StartY=1.47224 StartZ=0 EndX=-1.275 EndY=0.736122 EndZ=0
    g2: LineSegment StartX=-1.275 StartY=0.736122 StartZ=0 EndX=-1.275 EndY=-0.736122 EndZ=0
    g3: LineSegment StartX=-1.275 StartY=-0.736122 StartZ=0 EndX=1.34766e-11 EndY=-1.47224 EndZ=0
    g4: LineSegment StartX=1.34766e-11 StartY=-1.47224 StartZ=0 EndX=1.275 EndY=-0.736122 EndZ=0
    g5: LineSegment StartX=1.275 StartY=-0.736122 StartZ=0 EndX=1.275 EndY=0.736122 EndZ=0
    g6: Circle [constr] CenterX=0 CenterY=0 CenterZ=0 NormalX=0 NormalY=0 NormalZ=1 AngleXU=0 Radius=1.47224
  constraints (16):
    c: Coincident(g0,g1)
    c: Coincident(g1,g2)
    c: Coincident(g2,g3)
    c: Coincident(g3,g4)
    c: Coincident(g4,g5)
    c: Coincident(g5,g0)
    c: Equal(g0, g1-g5) x5
    c: PointOnObject(g0,g6)
    c: PointOnObject(g1,g6)
    c: PointOnObject(g2,g6)
    c: PointOnObject(g3,g6)
    c: PointOnObject(g4,g6)
    c: PointOnObject(g5,g6)
    c: Coincident(g6,g-1)
    c: PointOnObject(g0,g-2)
    c: DistanceX(g1,g0) = 2.55
FEATURE [PartDesign::Pocket] Pocket949  label="M3x8 Wrench199"
  BaseFeature = -> Pad1223
  Length = 1.3
  Length2 = 100
  Profile = -> Sketch2708
  Type = 0
FEATURE [PartDesign::Chamfer] Chamfer619  label="M3x8 Smooth198"
  Base = -> Pocket949 [Face11,Edge2,Edge24,Edge3]
  BaseFeature = -> Pocket949
  Size = 0.2
FEATURE [PartDesign::Body] Body816  label="M3x169"
  Group = -> [Sketch2705,Pad1224,Sketch2702,Pad1223,Sketch2708,Pocket949,Chamfer619]
  Origin = -> Origin1160
  Placement = pos=(-9e-15,-10,76.2) rot=(0,1,0;3.14159rad)
  Tip = -> Chamfer619
FEATURE [Sketcher::SketchObject] Sketch2709
  MapMode = 5
  Placement = pos=(0,0,3) rot=(0,0,1;0rad)
  Support = -> [Pad1220]
  sketch-geometry (1):
    g0: Circle CenterX=0 CenterY=0 CenterZ=0 NormalX=0 NormalY=0 NormalZ=1 AngleXU=0 Radius=1.5
  constraints (2):
    c: Coincident(g0,g-1)
    c: Radius(g0) = 1.5
FEATURE [PartDesign::Pad] Pad1222  label="M3x8 Thread199"
  BaseFeature = -> Pad1220
  Length = 8
  Length2 = 100
  Profile = -> Sketch2709
  Type = 0
FEATURE [Sketcher::SketchObject] Sketch2703
  MapMode = 5
  Placement = pos=(0,0,0) rot=(1,0,0;3.14159rad)
  Support = -> [Pad1222]
  sketch-geometry (7):
    g0: LineSegment StartX=1.275 StartY=0.736122 StartZ=0 EndX=0 EndY=1.47224 EndZ=0
    g1: LineSegment StartX=0 StartY=1.47224 StartZ=0 EndX=-1.275 EndY=0.736122 EndZ=0
    g2: LineSegment StartX=-1.275 StartY=0.736122 StartZ=0 EndX=-1.275 EndY=-0.736122 EndZ=0
    g3: LineSegment StartX=-1.275 StartY=-0.736122 StartZ=0 EndX=1.34766e-11 EndY=-1.47224 EndZ=0
    g4: LineSegment StartX=1.34766e-11 StartY=-1.47224 StartZ=0 EndX=1.275 EndY=-0.736122 EndZ=0
    g5: LineSegment StartX=1.275 StartY=-0.736122 StartZ=0 EndX=1.275 EndY=0.736122 EndZ=0
    g6: Circle [constr] CenterX=0 CenterY=0 CenterZ=0 NormalX=0 NormalY=0 NormalZ=1 AngleXU=0 Radius=1.47224
  constraints (16):
    c: Coincident(g0,g1)
    c: Coincident(g1,g2)
    c: Coincident(g2,g3)
    c: Coincident(g3,g4)
    c: Coincident(g4,g5)
    c: Coincident(g5,g0)
    c: Equal(g0, g1-g5) x5
    c: PointOnObject(g0,g6)
    c: PointOnObject(g1,g6)
    c: PointOnObject(g2,g6)
    c: PointOnObject(g3,g6)
    c: PointOnObject(g4,g6)
    c: PointOnObject(g5,g6)
    c: Coincident(g6,g-1)
    c: PointOnObject(g0,g-2)
    c: DistanceX(g1,g0) = 2.55
FEATURE [PartDesign::Pocket] Pocket952  label="M3x8 Wrench202"
  BaseFeature = -> Pad1222
  Length = 1.3
  Length2 = 100
  Profile = -> Sketch2703
  Type = 0
FEATURE [PartDesign::Chamfer] Chamfer621  label="M3x8 Smooth200"
  Base = -> Pocket952 [Face11,Edge2,Edge24,Edge3]
  BaseFeature = -> Pocket952
  Size = 0.2
FEATURE [PartDesign::Body] Body815  label="M3x168"
  Group = -> [Sketch2704,Pad1220,Sketch2709,Pad1222,Sketch2703,Pocket952,Chamfer621]
  Origin = -> Origin1157
  Placement = pos=(0,0,-4.25) rot=(0,0,1;0rad)
  Tip = -> Chamfer621
FEATURE [Sketcher::SketchObject] Sketch2710
  MapMode = 5
  Placement = pos=(0,0,0) rot=(1,0,0;3.14159rad)
  Support = -> [Pad1225]
  sketch-geometry (7):
    g0: LineSegment StartX=1.275 StartY=0.736122 StartZ=0 EndX=0 EndY=1.47224 EndZ=0
    g1: LineSegment StartX=0 StartY=1.47224 StartZ=0 EndX=-1.275 EndY=0.736122 EndZ=0
    g2: LineSegment StartX=-1.275 StartY=0.736122 StartZ=0 EndX=-1.275 EndY=-0.736122 EndZ=0
    g3: LineSegment StartX=-1.275 StartY=-0.736122 StartZ=0 EndX=1.34766e-11 EndY=-1.47224 EndZ=0
    g4: LineSegment StartX=1.34766e-11 StartY=-1.47224 StartZ=0 EndX=1.275 EndY=-0.736122 EndZ=0
    g5: LineSegment StartX=1.275 StartY=-0.736122 StartZ=0 EndX=1.275 EndY=0.736122 EndZ=0
    g6: Circle [constr] CenterX=0 CenterY=0 CenterZ=0 NormalX=0 NormalY=0 NormalZ=1 AngleXU=0 Radius=1.47224
  constraints (16):
    c: Coincident(g0,g1)
    c: Coincident(g1,g2)
    c: Coincident(g2,g3)
    c: Coincident(g3,g4)
    c: Coincident(g4,g5)
    c: Coincident(g5,g0)
    c: Equal(g0, g1-g5) x5
    c: PointOnObject(g0,g6)
    c: PointOnObject(g1,g6)
    c: PointOnObject(g2,g6)
    c: PointOnObject(g3,g6)
    c: PointOnObject(g4,g6)
    c: PointOnObject(g5,g6)
    c: Coincident(g6,g-1)
    c: PointOnObject(g0,g-2)
    c: DistanceX(g1,g0) = 2.55
FEATURE [PartDesign::Pocket] Pocket950  label="M3x8 Wrench200"
  BaseFeature = -> Pad1225
  Length = 1.3
  Length2 = 100
  Profile = -> Sketch2710
  Type = 0
FEATURE [PartDesign::Chamfer] Chamfer620  label="M3x8 Smooth199"
  Base = -> Pocket950 [Face11,Edge2,Edge24,Edge3]
  BaseFeature = -> Pocket950
  Size = 0.2
FEATURE [PartDesign::Body] Body817  label="M3x170"
  Group = -> [Sketch2707,Pad1226,Sketch2706,Pad1225,Sketch2710,Pocket950,Chamfer620]
  Origin = -> Origin1161
  Placement = pos=(0,10,-4.25) rot=(0,0,1;0rad)
  Tip = -> Chamfer620
FEATURE [Sketcher::SketchObject] Sketch2713
  MapMode = 5
  Support = -> [XY_Plane1159]
  sketch-geometry (1):
    g0: Circle CenterX=0 CenterY=0 CenterZ=0 NormalX=0 NormalY=0 NormalZ=1 AngleXU=0 Radius=2.75
  constraints (2):
    c: Coincident(g0,g-1)
    c: Radius(g0) = 2.75
FEATURE [PartDesign::Pad] Pad1221  label="M3x8 Head200"
  Length = 3
  Length2 = 100
  Profile = -> Sketch2713
  Type = 0
FEATURE [Sketcher::SketchObject] Sketch2711
  MapMode = 5
  Placement = pos=(0,0,3) rot=(0,0,1;0rad)
  Support = -> [Pad1221]
  sketch-geometry (1):
    g0: Circle CenterX=0 CenterY=0 CenterZ=0 NormalX=0 NormalY=0 NormalZ=1 AngleXU=0 Radius=1.5
  constraints (2):
    c: Coincident(g0,g-1)
    c: Radius(g0) = 1.5
FEATURE [PartDesign::Pad] Pad1227  label="M3x8 Thread202"
  BaseFeature = -> Pad1221
  Length = 8
  Length2 = 100
  Profile = -> Sketch2711
  Type = 0
FEATURE [Sketcher::SketchObject] Sketch2712
  MapMode = 5
  Placement = pos=(0,0,0) rot=(1,0,0;3.14159rad)
  Support = -> [Pad1227]
  sketch-geometry (7):
    g0: LineSegment StartX=1.275 StartY=0.736122 StartZ=0 EndX=0 EndY=1.47224 EndZ=0
    g1: LineSegment StartX=0 StartY=1.47224 StartZ=0 EndX=-1.275 EndY=0.736122 EndZ=0
    g2: LineSegment StartX=-1.275 StartY=0.736122 StartZ=0 EndX=-1.275 EndY=-0.736122 EndZ=0
    g3: LineSegment StartX=-1.275 StartY=-0.736122 StartZ=0 EndX=1.34766e-11 EndY=-1.47224 EndZ=0
    g4: LineSegment StartX=1.34766e-11 StartY=-1.47224 StartZ=0 EndX=1.275 EndY=-0.736122 EndZ=0
    g5: LineSegment StartX=1.275 StartY=-0.736122 StartZ=0 EndX=1.275 EndY=0.736122 EndZ=0
    g6: Circle [constr] CenterX=0 CenterY=0 CenterZ=0 NormalX=0 NormalY=0 NormalZ=1 AngleXU=0 Radius=1.47224
  constraints (16):
    c: Coincident(g0,g1)
    c: Coincident(g1,g2)
    c: Coincident(g2,g3)
    c: Coincident(g3,g4)
    c: Coincident(g4,g5)
    c: Coincident(g5,g0)
    c: Equal(g0, g1-g5) x5
    c: PointOnObject(g0,g6)
    c: PointOnObject(g1,g6)
    c: PointOnObject(g2,g6)
    c: PointOnObject(g3,g6)
    c: PointOnObject(g4,g6)
    c: PointOnObject(g5,g6)
    c: Coincident(g6,g-1)
    c: PointOnObject(g0,g-2)
    c: DistanceX(g1,g0) = 2.55
FEATURE [PartDesign::Pocket] Pocket951  label="M3x8 Wrench201"
  BaseFeature = -> Pad1227
  Length = 1.3
  Length2 = 100
  Profile = -> Sketch2712
  Type = 0
FEATURE [PartDesign::Chamfer] Chamfer622  label="M3x8 Smooth201"
  Base = -> Pocket951 [Face11,Edge2,Edge24,Edge3]
  BaseFeature = -> Pocket951
  Size = 0.2
FEATURE [PartDesign::Body] Body814  label="M3x167"
  Group = -> [Sketch2713,Pad1221,Sketch2711,Pad1227,Sketch2712,Pocket951,Chamfer622]
  Origin = -> Origin1159
  Placement = pos=(-9e-15,20.05,76.2) rot=(0,1,0;3.14159rad)
  Tip = -> Chamfer622
FEATURE [App::Part] Part322  label="Rear_Cover_Screws002"
  Group = -> [Body815,Body817,Body816,Body814]
  Origin = -> Origin1158
  Placement = pos=(-9,-104.5,165.6) rot=(0,0,1;0rad)
FEATURE [App::Part] Part321  label="Top and Bottom Cover Screws all"
  Group = -> [Part320,Part322]
  Origin = -> Origin1156
FEATURE [Sketcher::SketchObject] Sketch2716
  MapMode = 5
  Placement = pos=(0,0,0) rot=(1,0,0;1.5708rad)
  Support = -> [XZ_Plane1158]
  sketch-geometry (6):
    g0: LineSegment StartX=25 StartY=40 StartZ=0 EndX=85 EndY=40 EndZ=0
    g1: LineSegment StartX=110 StartY=15 StartZ=0 EndX=110 EndY=0 EndZ=0
    g2: LineSegment StartX=110 StartY=0 StartZ=0 EndX=0 EndY=0 EndZ=0
    g3: LineSegment StartX=0 StartY=0 StartZ=0 EndX=0 EndY=15 EndZ=0
    g4: ArcOfCircle CenterX=25 CenterY=15 CenterZ=0 NormalX=0 NormalY=0 NormalZ=1 AngleXU=0 Radius=25 StartAngle=1.5708 EndAngle=3.14159
    g5: ArcOfCircle CenterX=85 CenterY=15 CenterZ=0 NormalX=0 NormalY=0 NormalZ=1 AngleXU=0 Radius=25 StartAngle=0 EndAngle=1.5708
  constraints (15):
    c: Coincident(g1,g2)
    c: Coincident(g2,g3)
    c: Horizontal(g0)
    c: Horizontal(g2)
    c: Vertical(g1)
    c: Vertical(g3)
    c: Tangent(g3,g4) = 1.5708
    c: Tangent(g0,g4) = 1.5708
    c: Tangent(g0,g5) = 1.5708
    c: Tangent(g1,g5) = 1.5708
    c: DistanceX(g2,g2) = 110
    c: Equal(g5,g4)
    c: Radius(g4) = 25
    c: Coincident(g2,g-1)
    c: DistanceY(g2,g0) = 40
FEATURE [Sketcher::SketchObject] Sketch2719
  AttachmentOffset = pos=(0,0,-108.85) rot=(0,0,1;0rad)
  MapMode = 5
  Placement = pos=(0,108.85,2.42e-14) rot=(1,0,0;1.5708rad)
  Support = -> [XZ_Plane1158]
  sketch-geometry (14):
    g0: LineSegment StartX=0 StartY=15 StartZ=0 EndX=6.5 EndY=15 EndZ=0
    g1: LineSegment StartX=6.5 StartY=15 StartZ=0 EndX=6.5 EndY=31.8152 EndZ=0
    g2: ArcOfCircle CenterX=25 CenterY=15 CenterZ=0 NormalX=0 NormalY=0 NormalZ=1 AngleXU=0 Radius=25 StartAngle=2.40387 EndAngle=3.14159
    g3: LineSegment StartX=110 StartY=15 StartZ=0 EndX=103.5 EndY=15 EndZ=0
    g4: LineSegment StartX=103.5 StartY=15 StartZ=0 EndX=103.5 EndY=31.8152 EndZ=0
    g5: ArcOfCircle CenterX=85 CenterY=15 CenterZ=0 NormalX=0 NormalY=0 NormalZ=1 AngleXU=0 Radius=25 StartAngle=7e-16 EndAngle=0.737726
    g6: LineSegment StartX=36.75 StartY=40 StartZ=0 EndX=43.25 EndY=40 EndZ=0
    g7: LineSegment StartX=43.25 StartY=40 StartZ=0 EndX=43.25 EndY=33.5 EndZ=0
    g8: LineSegment StartX=43.25 StartY=33.5 StartZ=0 EndX=36.75 EndY=33.5 EndZ=0
    g9: LineSegment StartX=36.75 StartY=33.5 StartZ=0 EndX=36.75 EndY=40 EndZ=0
    g10: LineSegment StartX=66.75 StartY=40 StartZ=0 EndX=73.25 EndY=40 EndZ=0
    g11: LineSegment StartX=73.25 StartY=40 StartZ=0 EndX=73.25 EndY=33.5 EndZ=0
    g12: LineSegment StartX=73.25 StartY=33.5 StartZ=0 EndX=66.75 EndY=33.5 EndZ=0
    g13: LineSegment StartX=66.75 StartY=33.5 StartZ=0 EndX=66.75 EndY=40 EndZ=0
  constraints (44):
    c: PointOnObject(g0,g-2)
    c: Horizontal(g0)
    c: Coincident(g0,g1)
    c: Vertical(g1)
    c: Coincident(g2,g0)
    c: DistanceX(g0,g0) = 6.5
    c: Radius(g2) = 25
    c: DistanceY(g-1,g0) = 15
    c: Perpendicular(g2,g0)
    c: Coincident(g3,g4)
    c: Vertical(g4)
    c: Coincident(g5,g3)
    c: Horizontal(g3)
    c: Horizontal(g3,g0)
    c: Equal(g2,g5)
    c: Perpendicular(g5,g3)
    c: Equal(g3,g0)
    c: Coincident(g1,g2)
    c: Coincident(g4,g5)
    c: DistanceX(g0,g3) = 110
    c: Coincident(g6,g7)
    c: Coincident(g7,g8)
    c: Coincident(g8,g9)
    c: Coincident(g9,g6)
    c: Horizontal(g6)
    c: Horizontal(g8)
    c: Vertical(g7)
    c: Vertical(g9)
    c: Coincident(g10,g11)
    c: Coincident(g11,g12)
    c: Coincident(g12,g13)
    c: Coincident(g13,g10)
    c: Horizontal(g10)
    c: Horizontal(g12)
    c: Vertical(g11)
    c: Vertical(g13)
    c: Equal(g12,g8)
    c: Equal(g8,g3)
    c: Equal(g8,g7)
    c: Equal(g7,g13)
    c: Horizontal(g10,g6)
    c: DistanceX(g6,g10) = 23.5
    c: DistanceY(g-1,g6) = 40
    c: DistanceX(g-1,g8) = 36.75
FEATURE [Sketcher::SketchObject] Sketch2723
  AttachmentOffset = pos=(0,0,-108.85) rot=(0,0,1;0rad)
  MapMode = 5
  Placement = pos=(0,108.85,2.42e-14) rot=(1,0,0;1.5708rad)
  Support = -> [XZ_Plane1159]
  sketch-geometry (14):
    g0: LineSegment StartX=0 StartY=15 StartZ=0 EndX=6.5 EndY=15 EndZ=0
    g1: LineSegment StartX=6.5 StartY=15 StartZ=0 EndX=6.5 EndY=31.8152 EndZ=0
    g2: ArcOfCircle CenterX=25 CenterY=15 CenterZ=0 NormalX=0 NormalY=0 NormalZ=1 AngleXU=0 Radius=25 StartAngle=2.40387 EndAngle=3.14159
    g3: LineSegment StartX=110 StartY=15 StartZ=0 EndX=103.5 EndY=15 EndZ=0
    g4: LineSegment StartX=103.5 StartY=15 StartZ=0 EndX=103.5 EndY=31.8152 EndZ=0
    g5: ArcOfCircle CenterX=85 CenterY=15 CenterZ=0 NormalX=0 NormalY=0 NormalZ=1 AngleXU=0 Radius=25 StartAngle=7e-16 EndAngle=0.737726
    g6: LineSegment StartX=36.75 StartY=40 StartZ=0 EndX=43.25 EndY=40 EndZ=0
    g7: LineSegment StartX=43.25 StartY=40 StartZ=0 EndX=43.25 EndY=33.5 EndZ=0
    g8: LineSegment StartX=43.25 StartY=33.5 StartZ=0 EndX=36.75 EndY=33.5 EndZ=0
    g9: LineSegment StartX=36.75 StartY=33.5 StartZ=0 EndX=36.75 EndY=40 EndZ=0
    g10: LineSegment StartX=66.75 StartY=40 StartZ=0 EndX=73.25 EndY=40 EndZ=0
    g11: LineSegment StartX=73.25 StartY=40 StartZ=0 EndX=73.25 EndY=33.5 EndZ=0
    g12: LineSegment StartX=73.25 StartY=33.5 StartZ=0 EndX=66.75 EndY=33.5 EndZ=0
    g13: LineSegment StartX=66.75 StartY=33.5 StartZ=0 EndX=66.75 EndY=40 EndZ=0
  constraints (44):
    c: PointOnObject(g0,g-2)
    c: Horizontal(g0)
    c: Coincident(g0,g1)
    c: Vertical(g1)
    c: Coincident(g2,g0)
    c: DistanceX(g0,g0) = 6.5
    c: Radius(g2) = 25
    c: DistanceY(g-1,g0) = 15
    c: Perpendicular(g2,g0)
    c: Coincident(g3,g4)
    c: Vertical(g4)
    c: Coincident(g5,g3)
    c: Horizontal(g3)
    c: Horizontal(g3,g0)
    c: Equal(g2,g5)
    c: Perpendicular(g5,g3)
    c: Equal(g3,g0)
    c: Coincident(g1,g2)
    c: Coincident(g4,g5)
    c: DistanceX(g0,g3) = 110
    c: Coincident(g6,g7)
    c: Coincident(g7,g8)
    c: Coincident(g8,g9)
    c: Coincident(g9,g6)
    c: Horizontal(g6)
    c: Horizontal(g8)
    c: Vertical(g7)
    c: Vertical(g9)
    c: Coincident(g10,g11)
    c: Coincident(g11,g12)
    c: Coincident(g12,g13)
    c: Coincident(g13,g10)
    c: Horizontal(g10)
    c: Horizontal(g12)
    c: Vertical(g11)
    c: Vertical(g13)
    c: Equal(g12,g8)
    c: Equal(g8,g3)
    c: Equal(g8,g7)
    c: Equal(g7,g13)
    c: Horizontal(g10,g6)
    c: DistanceX(g6,g10) = 23.5
    c: DistanceY(g-1,g6) = 40
    c: DistanceX(g-1,g8) = 36.75
FEATURE [Sketcher::SketchObject] Sketch2726
  MapMode = 5
  Placement = pos=(0,0,0) rot=(1,0,0;1.5708rad)
  Support = -> [XZ_Plane1159]
  sketch-geometry (6):
    g0: LineSegment StartX=25 StartY=40 StartZ=0 EndX=85 EndY=40 EndZ=0
    g1: LineSegment StartX=110 StartY=15 StartZ=0 EndX=110 EndY=0 EndZ=0
    g2: LineSegment StartX=110 StartY=0 StartZ=0 EndX=0 EndY=0 EndZ=0
    g3: LineSegment StartX=0 StartY=0 StartZ=0 EndX=0 EndY=15 EndZ=0
    g4: ArcOfCircle CenterX=25 CenterY=15 CenterZ=0 NormalX=0 NormalY=0 NormalZ=1 AngleXU=0 Radius=25 StartAngle=1.5708 EndAngle=3.14159
    g5: ArcOfCircle CenterX=85 CenterY=15 CenterZ=0 NormalX=0 NormalY=0 NormalZ=1 AngleXU=0 Radius=25 StartAngle=0 EndAngle=1.5708
  constraints (15):
    c: Coincident(g1,g2)
    c: Coincident(g2,g3)
    c: Horizontal(g0)
    c: Horizontal(g2)
    c: Vertical(g1)
    c: Vertical(g3)
    c: Tangent(g3,g4) = 1.5708
    c: Tangent(g0,g4) = 1.5708
    c: Tangent(g0,g5) = 1.5708
    c: Tangent(g1,g5) = 1.5708
    c: DistanceX(g2,g2) = 110
    c: Equal(g5,g4)
    c: Radius(g4) = 25
    c: Coincident(g2,g-1)
    c: DistanceY(g2,g0) = 40
FEATURE [Sketcher::SketchObject] Sketch2736
  MapMode = 5
  Support = -> [XY_Plane1168]
  sketch-geometry (1):
    g0: Circle CenterX=0 CenterY=0 CenterZ=0 NormalX=0 NormalY=0 NormalZ=1 AngleXU=0 Radius=2.75
  constraints (2):
    c: Coincident(g0,g-1)
    c: Radius(g0) = 2.75
FEATURE [Sketcher::SketchObject] Sketch2737
  MapMode = 5
  Support = -> [XY_Plane1171]
  sketch-geometry (8):
    g0: LineSegment StartX=0 StartY=3.17543 StartZ=0 EndX=-2.75 EndY=1.58771 EndZ=0
    g1: LineSegment StartX=-2.75 StartY=1.58771 StartZ=0 EndX=-2.75 EndY=-1.58771 EndZ=0
    g2: LineSegment StartX=-2.75 StartY=-1.58771 StartZ=0 EndX=0 EndY=-3.17543 EndZ=0
    g3: LineSegment StartX=0 StartY=-3.17543 StartZ=0 EndX=2.75 EndY=-1.58771 EndZ=0
    g4: LineSegment StartX=2.75 StartY=-1.58771 StartZ=0 EndX=2.75 EndY=1.58771 EndZ=0
    g5: LineSegment StartX=2.75 StartY=1.58771 StartZ=0 EndX=0 EndY=3.17543 EndZ=0
    g6: Circle [constr] CenterX=0 CenterY=0 CenterZ=0 NormalX=0 NormalY=0 NormalZ=1 AngleXU=0 Radius=3.17543
    g7: Circle CenterX=0 CenterY=0 CenterZ=0 NormalX=0 NormalY=0 NormalZ=1 AngleXU=0 Radius=1.5
  constraints (18):
    c: Coincident(g0,g1)
    c: Coincident(g1,g2)
    c: Coincident(g2,g3)
    c: Coincident(g3,g4)
    c: Coincident(g4,g5)
    c: Coincident(g5,g0)
    c: Equal(g0, g1-g5) x5
    c: PointOnObject(g0,g6)
    c: PointOnObject(g1,g6)
    c: PointOnObject(g2,g6)
    c: PointOnObject(g3,g6)
    c: PointOnObject(g4,g6)
    c: PointOnObject(g5,g6)
    c: Coincident(g6,g-1)
    c: PointOnObject(g5,g-2)
    c: DistanceX(g0,g4) = 5.5
    c: Coincident(g7,g-1)
    c: Radius(g7) = 1.5
FEATURE [Sketcher::SketchObject] Sketch2739
  MapMode = 5
  Support = -> [XY_Plane1163]
  sketch-geometry (8):
    g0: LineSegment StartX=0 StartY=3.17543 StartZ=0 EndX=-2.75 EndY=1.58771 EndZ=0
    g1: LineSegment StartX=-2.75 StartY=1.58771 StartZ=0 EndX=-2.75 EndY=-1.58771 EndZ=0
    g2: LineSegment StartX=-2.75 StartY=-1.58771 StartZ=0 EndX=0 EndY=-3.17543 EndZ=0
    g3: LineSegment StartX=0 StartY=-3.17543 StartZ=0 EndX=2.75 EndY=-1.58771 EndZ=0
    g4: LineSegment StartX=2.75 StartY=-1.58771 StartZ=0 EndX=2.75 EndY=1.58771 EndZ=0
    g5: LineSegment StartX=2.75 StartY=1.58771 StartZ=0 EndX=0 EndY=3.17543 EndZ=0
    g6: Circle [constr] CenterX=0 CenterY=0 CenterZ=0 NormalX=0 NormalY=0 NormalZ=1 AngleXU=0 Radius=3.17543
    g7: Circle CenterX=0 CenterY=0 CenterZ=0 NormalX=0 NormalY=0 NormalZ=1 AngleXU=0 Radius=1.5
  constraints (18):
    c: Coincident(g0,g1)
    c: Coincident(g1,g2)
    c: Coincident(g2,g3)
    c: Coincident(g3,g4)
    c: Coincident(g4,g5)
    c: Coincident(g5,g0)
    c: Equal(g0, g1-g5) x5
    c: PointOnObject(g0,g6)
    c: PointOnObject(g1,g6)
    c: PointOnObject(g2,g6)
    c: PointOnObject(g3,g6)
    c: PointOnObject(g4,g6)
    c: PointOnObject(g5,g6)
    c: Coincident(g6,g-1)
    c: PointOnObject(g5,g-2)
    c: DistanceX(g0,g4) = 5.5
    c: Coincident(g7,g-1)
    c: Radius(g7) = 1.5
FEATURE [PartDesign::Pad] Pad1232  label="Baseplate051"
  Length = 160
  Length2 = 100
  Placement = pos=(0,0,0) rot=(1,0,0;1.5708rad)
  Profile = -> Sketch2726
  Reversed = true
  Type = 0
FEATURE [PartDesign::Pad] Pad1236  label="Baseplate052"
  Length = 160
  Length2 = 100
  Placement = pos=(0,0,0) rot=(1,0,0;1.5708rad)
  Profile = -> Sketch2716
  Reversed = true
  Type = 0
FEATURE [PartDesign::Pad] Pad1237  label="M3x8 Head204"
  Length = 3
  Length2 = 100
  Profile = -> Sketch2736
  Type = 0
FEATURE [PartDesign::Pad] Pad1240  label="M3 Nut Primitive254"
  Length = 1.2
  Length2 = 1.2
  Profile = -> Sketch2737
  Type = 4
FEATURE [Sketcher::SketchObject] Sketch2732
  ExternalGeometry = -> [Pad1240]
  MapMode = 5
  Placement = pos=(0,0,0) rot=(0.57735,0.57735,0.57735;2.0944rad)
  Support = -> [YZ_Plane1165]
  sketch-geometry (6):
    g0: LineSegment StartX=-2.67543 StartY=1.2 StartZ=0 EndX=-3.67543 EndY=1.2 EndZ=0
    g1: LineSegment StartX=-3.67543 StartY=1.2 StartZ=0 EndX=-3.67543 EndY=-1.2 EndZ=0
    g2: LineSegment StartX=-3.67543 StartY=-1.2 StartZ=0 EndX=-2.67543 EndY=-1.2 EndZ=0
    g3: LineSegment StartX=-2.67543 StartY=-1.2 StartZ=0 EndX=-3.17543 EndY=-1 EndZ=0
    g4: LineSegment StartX=-3.17543 StartY=-1 StartZ=0 EndX=-3.17543 EndY=1 EndZ=0
    g5: LineSegment StartX=-3.17543 StartY=1 StartZ=0 EndX=-2.67543 EndY=1.2 EndZ=0
  constraints (15):
    c: Horizontal(g0)
    c: Coincident(g0,g1)
    c: Coincident(g1,g2)
    c: Coincident(g2,g3)
    c: Coincident(g3,g4)
    c: Coincident(g4,g5)
    c: Coincident(g5,g0)
    c: Symmetric(g4,g3,g-1)
    c: Symmetric(g0,g2,g-1)
    c: Symmetric(g1,g0,g-1)
    c: DistanceX(g0,g4) = 0.5
    c: DistanceY(g3,g4) = 2
    c: DistanceY(g1,g0) = 2.4
    c: PointOnObject(g3,g-3)
    c: DistanceX(g4,g0) = 0.5
FEATURE [PartDesign::Groove] Groove264  label="M3 Nut Smooth255"
  Angle = 360
  Axis = (-2e-16,3e-16,1)
  Base = (0,0,0)
  BaseFeature = -> Pad1240
  Profile = -> Sketch2732
  ReferenceAxis = -> Sketch2732 [V_Axis]
  Reversed = true
FEATURE [PartDesign::Chamfer] Chamfer627  label="M3 Nut Smooth Hole254"
  Base = -> Groove264 [Edge24,Edge23]
  BaseFeature = -> Groove264
  Size = 0.2
FEATURE [PartDesign::Body] Body823  label="M3 Nut155"
  Group = -> [Sketch2737,Pad1240,Sketch2732,Groove264,Chamfer627]
  Origin = -> Origin1171
  Placement = pos=(103.5,-5,0) rot=(0,0,1;0rad)
  Tip = -> Chamfer627
FEATURE [PartDesign::Pad] Pad1242  label="M3 Nut Primitive256"
  Length = 1.2
  Length2 = 1.2
  Profile = -> Sketch2739
  Type = 4
FEATURE [Sketcher::SketchObject] Sketch2733
  ExternalGeometry = -> [Pad1242]
  MapMode = 5
  Placement = pos=(0,0,0) rot=(0.57735,0.57735,0.57735;2.0944rad)
  Support = -> [YZ_Plane1167]
  sketch-geometry (6):
    g0: LineSegment StartX=-2.67543 StartY=1.2 StartZ=0 EndX=-3.67543 EndY=1.2 EndZ=0
    g1: LineSegment StartX=-3.67543 StartY=1.2 StartZ=0 EndX=-3.67543 EndY=-1.2 EndZ=0
    g2: LineSegment StartX=-3.67543 StartY=-1.2 StartZ=0 EndX=-2.67543 EndY=-1.2 EndZ=0
    g3: LineSegment StartX=-2.67543 StartY=-1.2 StartZ=0 EndX=-3.17543 EndY=-1 EndZ=0
    g4: LineSegment StartX=-3.17543 StartY=-1 StartZ=0 EndX=-3.17543 EndY=1 EndZ=0
    g5: LineSegment StartX=-3.17543 StartY=1 StartZ=0 EndX=-2.67543 EndY=1.2 EndZ=0
  constraints (15):
    c: Horizontal(g0)
    c: Coincident(g0,g1)
    c: Coincident(g1,g2)
    c: Coincident(g2,g3)
    c: Coincident(g3,g4)
    c: Coincident(g4,g5)
    c: Coincident(g5,g0)
    c: Symmetric(g4,g3,g-1)
    c: Symmetric(g0,g2,g-1)
    c: Symmetric(g1,g0,g-1)
    c: DistanceX(g0,g4) = 0.5
    c: DistanceY(g3,g4) = 2
    c: DistanceY(g1,g0) = 2.4
    c: PointOnObject(g3,g-3)
    c: DistanceX(g4,g0) = 0.5
FEATURE [PartDesign::Groove] Groove262  label="M3 Nut Smooth253"
  Angle = 360
  Axis = (-2e-16,3e-16,1)
  Base = (0,0,0)
  BaseFeature = -> Pad1242
  Profile = -> Sketch2733
  ReferenceAxis = -> Sketch2733 [V_Axis]
  Reversed = true
FEATURE [PartDesign::Chamfer] Chamfer626  label="M3 Nut Smooth Hole253"
  Base = -> Groove262 [Edge24,Edge23]
  BaseFeature = -> Groove262
  Size = 0.2
FEATURE [PartDesign::Body] Body822  label="M3 Nut154"
  Group = -> [Sketch2739,Pad1242,Sketch2733,Groove262,Chamfer626]
  Origin = -> Origin1169
  Placement = pos=(66.75,13.5,0) rot=(0,0,1;0rad)
  Tip = -> Chamfer626
FEATURE [PartDesign::Thickness] Thickness004
  Base = -> Pad1232 [Face7,Face8,Face2]
  BaseFeature = -> Pad1232
  Join = 0
  Mode = 0
  Value = 2
FEATURE [PartDesign::Pad] Pad1231  label="Front Expansion003"
  BaseFeature = -> Thickness004
  Length = 23.75
  Length2 = 100
  Profile = -> Thickness004 [Face6]
  Type = 0
FEATURE [PartDesign::Pad] Pad1228  label="Rear Expansion003"
  BaseFeature = -> Pad1231
  Length = 23.75
  Length2 = 100
  Profile = -> Pad1231 [Face5]
  Type = 0
FEATURE [Sketcher::SketchObject] Sketch2730
  MapMode = 5
  Placement = pos=(0,-9.2e-15,42) rot=(0,0,1;0rad)
  Support = -> [Pad1228]
  sketch-geometry (16):
    g0: LineSegment StartX=-2 StartY=0 StartZ=0 EndX=40 EndY=0 EndZ=0
    g1: LineSegment StartX=40 StartY=0 StartZ=0 EndX=40 EndY=-23.75 EndZ=0
    g2: LineSegment StartX=40 StartY=-23.75 StartZ=0 EndX=-2 EndY=-23.75 EndZ=0
    g3: LineSegment StartX=-2 StartY=-23.75 StartZ=0 EndX=-2 EndY=0 EndZ=0
    g4: LineSegment StartX=112 StartY=0 StartZ=0 EndX=70 EndY=0 EndZ=0
    g5: LineSegment StartX=70 StartY=0 StartZ=0 EndX=70 EndY=-23.75 EndZ=0
    g6: LineSegment StartX=70 StartY=-23.75 StartZ=0 EndX=112 EndY=-23.75 EndZ=0
    g7: LineSegment StartX=112 StartY=-23.75 StartZ=0 EndX=112 EndY=0 EndZ=0
    g8: LineSegment StartX=-2 StartY=160 StartZ=0 EndX=40 EndY=160 EndZ=0
    g9: LineSegment StartX=40 StartY=160 StartZ=0 EndX=40 EndY=183.75 EndZ=0
    g10: LineSegment StartX=40 StartY=183.75 StartZ=0 EndX=-2 EndY=183.75 EndZ=0
    g11: LineSegment StartX=-2 StartY=183.75 StartZ=0 EndX=-2 EndY=160 EndZ=0
    g12: LineSegment StartX=112 StartY=183.75 StartZ=0 EndX=70 EndY=183.75 EndZ=0
    g13: LineSegment StartX=70 StartY=183.75 StartZ=0 EndX=70 EndY=160 EndZ=0
    g14: LineSegment StartX=70 StartY=160 StartZ=0 EndX=112 EndY=160 EndZ=0
    g15: LineSegment StartX=112 StartY=160 StartZ=0 EndX=112 EndY=183.75 EndZ=0
  constraints (48):
    c: Coincident(g0,g1)
    c: Coincident(g1,g2)
    c: Coincident(g2,g3)
    c: Coincident(g3,g0)
    c: Horizontal(g0)
    c: Horizontal(g2)
    c: Vertical(g1)
    c: Vertical(g3)
    c: PointOnObject(g0,g-1)
    c: Coincident(g4,g5)
    c: Coincident(g5,g6)
    c: Coincident(g6,g7)
    c: Coincident(g7,g4)
    c: Horizontal(g4)
    c: Horizontal(g6)
    c: Vertical(g5)
    c: Vertical(g7)
    c: Coincident(g8,g9)
    c: Coincident(g9,g10)
    c: Coincident(g10,g11)
    c: Coincident(g11,g8)
    c: Horizontal(g8)
    c: Horizontal(g10)
    c: Vertical(g9)
    c: Vertical(g11)
    c: Coincident(g12,g13)
    c: Coincident(g13,g14)
    c: Coincident(g14,g15)
    c: Coincident(g15,g12)
    c: Horizontal(g12)
    c: Horizontal(g14)
    c: Vertical(g13)
    c: Vertical(g15)
    c: Horizontal(g9,g12)
    c: Equal(g9,g13)
    c: Equal(g10,g12)
    c: Equal(g0,g8)
    c: Equal(g4,g14)
    c: Horizontal(g0,g4)
    c: Equal(g5,g1)
    c: DistanceX(g0,g4) = 30
    c: DistanceX(g0,g0) = 42
    c: DistanceY(g3,g3) = 23.75
    c: DistanceX(g0,g-1) = 2
    c: Vertical(g0,g8)
    c: Vertical(g13,g4)
    c: DistanceY(g0,g8) = 160
    c: Equal(g9,g1)
FEATURE [PartDesign::Pocket] Pocket960  label="Shoulders004"
  BaseFeature = -> Pad1228
  Length = 42
  Length2 = 100
  Profile = -> Sketch2730
  Type = 0
FEATURE [Sketcher::SketchObject] Sketch2728
  MapMode = 5
  Placement = pos=(112,0,0) rot=(0.57735,0.57735,0.57735;2.0944rad)
  Support = -> [Pocket960]
  sketch-geometry (6):
    g0: LineSegment StartX=0 StartY=-5 StartZ=0 EndX=-2e-16 EndY=12 EndZ=0
    g1: LineSegment StartX=-2e-16 StartY=12 StartZ=0 EndX=75 EndY=12 EndZ=0
    g2: LineSegment StartX=75 StartY=12 StartZ=0 EndX=105 EndY=0 EndZ=0
    g3: LineSegment StartX=105 StartY=0 StartZ=0 EndX=160 EndY=0 EndZ=0
    g4: LineSegment StartX=160 StartY=0 StartZ=0 EndX=160 EndY=-5 EndZ=0
    g5: LineSegment StartX=160 StartY=-5 StartZ=0 EndX=0 EndY=-5 EndZ=0
  constraints (18):
    c: PointOnObject(g0,g-2)
    c: Coincident(g0,g1)
    c: Horizontal(g1)
    c: Coincident(g1,g2)
    c: PointOnObject(g2,g-1)
    c: Coincident(g2,g3)
    c: Horizontal(g3)
    c: Coincident(g3,g4)
    c: Vertical(g4)
    c: Coincident(g4,g5)
    c: PointOnObject(g5,g-2)
    c: Horizontal(g5)
    c: Coincident(g0,g5)
    c: DistanceX(g1,g2) = 30
    c: DistanceX(g5,g5) = 160
    c: DistanceX(g1,g1) = 75
    c: DistanceY(g-1,g0) = 12
    c: DistanceY(g4,g4) = 5
FEATURE [PartDesign::Pocket] Pocket956  label="Side Detailing004"
  BaseFeature = -> Pocket960
  Length = 114
  Length2 = 100
  Profile = -> Sketch2728
  Type = 0
FEATURE [Sketcher::SketchObject] Sketch2727
  MapMode = 5
  Placement = pos=(0,-9.2e-15,42) rot=(0,0,1;0rad)
  Support = -> [Pocket956]
  sketch-geometry (4):
    g0: Circle CenterX=50 CenterY=-18.75 CenterZ=0 NormalX=0 NormalY=0 NormalZ=1 AngleXU=0 Radius=1.6
    g1: Circle CenterX=60 CenterY=-18.75 CenterZ=0 NormalX=0 NormalY=0 NormalZ=1 AngleXU=0 Radius=1.6
    g2: Circle CenterX=50 CenterY=178.75 CenterZ=0 NormalX=0 NormalY=0 NormalZ=1 AngleXU=0 Radius=1.6
    g3: Circle CenterX=60 CenterY=178.75 CenterZ=0 NormalX=0 NormalY=0 NormalZ=1 AngleXU=0 Radius=1.6
  constraints (12):
    c: DistanceX(g2,g3) = 10
    c: Equal(g2,g3)
    c: Equal(g3,g0)
    c: Equal(g0,g1)
    c: Horizontal(g2,g3)
    c: Horizontal(g0,g1)
    c: Vertical(g1,g3)
    c: Vertical(g0,g2)
    c: DistanceY(g0,g-1) = 18.75
    c: DistanceX(g-1,g0) = 50
    c: DistanceY(g-1,g2) = 178.75
    c: Radius(g3) = 1.6
FEATURE [PartDesign::Pocket] Pocket957  label="Screwholes014"
  BaseFeature = -> Pocket956
  Length = 2
  Length2 = 100
  Profile = -> Sketch2727
  Type = 0
FEATURE [PartDesign::Fillet] Fillet284  label="Round Corners003"
  Base = -> Pocket957 [Edge35,Edge66,Edge48,Edge12,Edge18,Edge44,Edge25,Edge76,Edge57,Edge60,Edge45,Edge9]
  BaseFeature = -> Pocket957
  Radius = 5
FEATURE [PartDesign::Fillet] Fillet281  label="Round Side Details003"
  Base = -> Fillet284 [Edge10,Edge16,Edge131,Edge132]
  BaseFeature = -> Fillet284
  Radius = 20
FEATURE [PartDesign::Pad] Pad1233  label="Screwpads004"
  BaseFeature = -> Fillet281
  Length = 5.5
  Length2 = 5.5
  Profile = -> Sketch2723
  Type = 4
FEATURE [PartDesign::Fillet] Fillet282  label="Smooth Screwpad Edges003"
  Base = -> Pad1233 [Edge169,Edge130,Edge126,Edge122,Edge118,Edge29,Edge27,Edge97,Edge65,Edge61,Edge63,Edge59]
  BaseFeature = -> Pad1233
  Radius = 1
FEATURE [PartDesign::Fillet] Fillet283  label="Smooth Screwpad Edges Side Details003"
  Base = -> Fillet282 [Edge207,Edge22]
  BaseFeature = -> Fillet282
  Radius = 0.2
FEATURE [Sketcher::SketchObject] Sketch2724
  MapMode = 5
  Placement = pos=(0,114.35,0) rot=(0,0.707107,0.707107;3.14159rad)
  Support = -> [Fillet283]
  sketch-geometry (4):
    g0: Circle CenterX=-106.75 CenterY=18.25 CenterZ=0 NormalX=0 NormalY=0 NormalZ=1 AngleXU=0 Radius=1.6
    g1: Circle CenterX=-70 CenterY=36.75 CenterZ=0 NormalX=0 NormalY=0 NormalZ=1 AngleXU=0 Radius=1.6
    g2: Circle CenterX=-40 CenterY=36.75 CenterZ=0 NormalX=0 NormalY=0 NormalZ=1 AngleXU=0 Radius=1.6
    g3: Circle CenterX=-3.25 CenterY=18.25 CenterZ=0 NormalX=0 NormalY=0 NormalZ=1 AngleXU=0 Radius=1.6
  constraints (12):
    c: Equal(g0,g1)
    c: Equal(g1,g2)
    c: Equal(g2,g3)
    c: Radius(g3) = 1.6
    c: Horizontal(g1,g2)
    c: Horizontal(g0,g3)
    c: DistanceX(g3,g-1) = 3.25
    c: DistanceY(g-1,g3) = 18.25
    c: DistanceX(g0,g3) = 103.5
    c: DistanceX(g1,g2) = 30
    c: DistanceY(g-1,g2) = 36.75
    c: DistanceX(g2,g-1) = 40
FEATURE [PartDesign::Pocket] Pocket953  label="Screwholes Connection003"
  BaseFeature = -> Fillet283
  Length = 11
  Length2 = 100
  Profile = -> Sketch2724
  Type = 0
FEATURE [Sketcher::SketchObject] Sketch2725
  MapMode = 5
  Placement = pos=(0,114.35,0) rot=(0,0.707107,0.707107;3.14159rad)
  Support = -> [Pocket953]
  sketch-geometry (4):
    g0: Circle CenterX=-106.75 CenterY=18.25 CenterZ=0 NormalX=0 NormalY=0 NormalZ=1 AngleXU=0 Radius=2.85
    g1: Circle CenterX=-70 CenterY=36.75 CenterZ=0 NormalX=0 NormalY=0 NormalZ=1 AngleXU=0 Radius=2.85
    g2: Circle CenterX=-40 CenterY=36.75 CenterZ=0 NormalX=0 NormalY=0 NormalZ=1 AngleXU=0 Radius=2.85
    g3: Circle CenterX=-3.25 CenterY=18.25 CenterZ=0 NormalX=0 NormalY=0 NormalZ=1 AngleXU=0 Radius=2.85
  constraints (12):
    c: Equal(g3,g2)
    c: Equal(g2,g1)
    c: Equal(g1,g0)
    c: Radius(g3) = 2.85
    c: DistanceX(g3,g-1) = 3.25
    c: DistanceY(g-1,g3) = 18.25
    c: Horizontal(g3,g0)
    c: DistanceX(g0,g3) = 103.5
    c: DistanceX(g1,g2) = 30
    c: DistanceY(g-1,g2) = 36.75
    c: DistanceX(g2,g-1) = 40
    c: Horizontal(g1,g2)
FEATURE [PartDesign::Pocket] Pocket959  label="Screwheads Connection003"
  BaseFeature = -> Pocket953
  Length = 3
  Length2 = 100
  Profile = -> Sketch2725
  Type = 0
FEATURE [Sketcher::SketchObject] Sketch2731
  MapMode = 5
  Placement = pos=(0,103.35,0) rot=(1,0,0;1.5708rad)
  Support = -> [Pocket959]
  sketch-geometry (28):
    g0: LineSegment StartX=3.25 StartY=21.5409 StartZ=0 EndX=0.4 EndY=19.8954 EndZ=0
    g1: LineSegment StartX=0.4 StartY=19.8954 StartZ=0 EndX=0.4 EndY=16.6046 EndZ=0
    g2: LineSegment StartX=0.4 StartY=16.6046 StartZ=0 EndX=3.25 EndY=14.9591 EndZ=0
    g3: LineSegment StartX=3.25 StartY=14.9591 StartZ=0 EndX=6.1 EndY=16.6046 EndZ=0
    g4: LineSegment StartX=6.1 StartY=16.6046 StartZ=0 EndX=6.1 EndY=19.8954 EndZ=0
    g5: LineSegment StartX=6.1 StartY=19.8954 StartZ=0 EndX=3.25 EndY=21.5409 EndZ=0
    g6: Circle [constr] CenterX=3.25 CenterY=18.25 CenterZ=0 NormalX=0 NormalY=0 NormalZ=1 AngleXU=0 Radius=3.2909
    g7: LineSegment StartX=42.85 StartY=38.3954 StartZ=0 EndX=40 EndY=40.0409 EndZ=0
    g8: LineSegment StartX=40 StartY=40.0409 StartZ=0 EndX=37.15 EndY=38.3954 EndZ=0
    g9: LineSegment StartX=37.15 StartY=38.3954 StartZ=0 EndX=37.15 EndY=35.1046 EndZ=0
    g10: LineSegment StartX=37.15 StartY=35.1046 StartZ=0 EndX=40 EndY=33.4591 EndZ=0
    g11: LineSegment StartX=40 StartY=33.4591 StartZ=0 EndX=42.85 EndY=35.1046 EndZ=0
    g12: LineSegment StartX=42.85 StartY=35.1046 StartZ=0 EndX=42.85 EndY=38.3954 EndZ=0
    g13: Circle [constr] CenterX=40 CenterY=36.75 CenterZ=0 NormalX=0 NormalY=0 NormalZ=1 AngleXU=0 Radius=3.2909
    g14: LineSegment StartX=72.85 StartY=38.3954 StartZ=0 EndX=70 EndY=40.0409 EndZ=0
    g15: LineSegment StartX=70 StartY=40.0409 StartZ=0 EndX=67.15 EndY=38.3954 EndZ=0
    g16: LineSegment StartX=67.15 StartY=38.3954 StartZ=0 EndX=67.15 EndY=35.1046 EndZ=0
    g17: LineSegment StartX=67.15 StartY=35.1046 StartZ=0 EndX=70 EndY=33.4591 EndZ=0
    g18: LineSegment StartX=70 StartY=33.4591 StartZ=0 EndX=72.85 EndY=35.1046 EndZ=0
    g19: LineSegment StartX=72.85 StartY=35.1046 StartZ=0 EndX=72.85 EndY=38.3954 EndZ=0
    g20: Circle [constr] CenterX=70 CenterY=36.75 CenterZ=0 NormalX=0 NormalY=0 NormalZ=1 AngleXU=0 Radius=3.2909
    g21: LineSegment StartX=106.75 StartY=21.5409 StartZ=0 EndX=103.9 EndY=19.8954 EndZ=0
    g22: LineSegment StartX=103.9 StartY=19.8954 StartZ=0 EndX=103.9 EndY=16.6046 EndZ=0
    g23: LineSegment StartX=103.9 StartY=16.6046 StartZ=0 EndX=106.75 EndY=14.9591 EndZ=0
    g24: LineSegment StartX=106.75 StartY=14.9591 StartZ=0 EndX=109.6 EndY=16.6046 EndZ=0
    g25: LineSegment StartX=109.6 StartY=16.6046 StartZ=0 EndX=109.6 EndY=19.8954 EndZ=0
    g26: LineSegment StartX=109.6 StartY=19.8954 StartZ=0 EndX=106.75 EndY=21.5409 EndZ=0
    g27: Circle [constr] CenterX=106.75 CenterY=18.25 CenterZ=0 NormalX=0 NormalY=0 NormalZ=1 AngleXU=0 Radius=3.2909
  constraints (68):
    c: Coincident(g0,g1)
    c: Coincident(g1,g2)
    c: Coincident(g2,g3)
    c: Coincident(g3,g4)
    c: Coincident(g4,g5)
    c: Coincident(g5,g0)
    c: Equal(g0, g1-g5) x5
    c: PointOnObject(g0,g6)
    c: PointOnObject(g1,g6)
    c: PointOnObject(g2,g6)
    c: PointOnObject(g3,g6)
    c: PointOnObject(g4,g6)
    c: PointOnObject(g5,g6)
    c: Coincident(g7,g8)
    c: Coincident(g8,g9)
    c: Coincident(g9,g10)
    c: Coincident(g10,g11)
    c: Coincident(g11,g12)
    c: Coincident(g12,g7)
    c: Equal(g7, g8-g12) x5
    c: PointOnObject(g7,g13)
    c: PointOnObject(g8,g13)
    c: PointOnObject(g9,g13)
    c: PointOnObject(g10,g13)
    c: PointOnObject(g11,g13)
    c: PointOnObject(g12,g13)
    c: Coincident(g14,g15)
    c: Coincident(g15,g16)
    c: Coincident(g16,g17)
    c: Coincident(g17,g18)
    c: Coincident(g18,g19)
    c: Coincident(g19,g14)
    c: Equal(g14, g15-g19) x5
    c: PointOnObject(g14,g20)
    c: PointOnObject(g15,g20)
    c: PointOnObject(g16,g20)
    c: PointOnObject(g17,g20)
    c: PointOnObject(g18,g20)
    c: PointOnObject(g19,g20)
    c: Coincident(g21,g22)
    c: Coincident(g22,g23)
    c: Coincident(g23,g24)
    c: Coincident(g24,g25)
    c: Coincident(g25,g26)
    c: Coincident(g26,g21)
    c: Equal(g21, g22-g26) x5
    c: PointOnObject(g21,g27)
    c: PointOnObject(g22,g27)
    c: PointOnObject(g23,g27)
    c: PointOnObject(g24,g27)
    c: PointOnObject(g25,g27)
    c: PointOnObject(g26,g27)
    c: Vertical(g12)
    c: Vertical(g16)
    c: Vertical(g4)
    c: Vertical(g22)
    c: Equal(g27,g20)
    c: Equal(g20,g13)
    c: Equal(g13,g6)
    c: DistanceX(g21,g25) = 5.7
    c: DistanceX(g-1,g6) = 3.25
    c: DistanceY(g-1,g6) = 18.25
    c: DistanceX(g6,g27) = 103.5
    c: Horizontal(g27,g6)
    c: Horizontal(g13,g20)
    c: DistanceX(g13,g20) = 30
    c: DistanceY(g-1,g13) = 36.75
    c: DistanceX(g-1,g13) = 40
FEATURE [PartDesign::Pocket] Pocket958  label="Nutholes Connection003"
  BaseFeature = -> Pocket959
  Length = 2.5
  Length2 = 100
  Profile = -> Sketch2731
  Type = 0
FEATURE [Sketcher::SketchObject] Sketch2729
  MapMode = 5
  Placement = pos=(112,0,0) rot=(0.57735,0.57735,0.57735;2.0944rad)
  Support = -> [Pocket958]
  sketch-geometry (4):
    g0: LineSegment StartX=-23.75 StartY=0 StartZ=0 EndX=108.85 EndY=0 EndZ=0
    g1: LineSegment StartX=108.85 StartY=0 StartZ=0 EndX=108.85 EndY=42 EndZ=0
    g2: LineSegment StartX=108.85 StartY=42 StartZ=0 EndX=-23.75 EndY=42 EndZ=0
    g3: LineSegment StartX=-23.75 StartY=42 StartZ=0 EndX=-23.75 EndY=0 EndZ=0
  constraints (12):
    c: Coincident(g0,g1)
    c: Coincident(g1,g2)
    c: Coincident(g2,g3)
    c: Coincident(g3,g0)
    c: Horizontal(g0)
    c: Horizontal(g2)
    c: Vertical(g1)
    c: Vertical(g3)
    c: PointOnObject(g0,g-1)
    c: DistanceX(g-1,g0) = 108.85
    c: DistanceY(g3,g3) = 42
    c: DistanceX(g0,g-1) = 23.75
FEATURE [PartDesign::Pocket] Pocket962  label="Remove Front001"
  BaseFeature = -> Pocket958
  Length = 114
  Length2 = 100
  Profile = -> Sketch2729
  Type = 0
FEATURE [PartDesign::Body] Body818  label="Bottom_Cover_Split_Rear"
  Group = -> [Sketch2726,Pad1232,Thickness004,Pad1231,Pad1228,Sketch2730,Pocket960,Sketch2728,Pocket956,Sketch2727,Pocket957,Fillet284,Fillet281,Sketch2723,Pad1233,Fillet282,Fillet283,Sketch2724,Pocket953,Sketch2725,Pocket959,Sketch2731,Pocket958,Sketch2729,Pocket962]
  Origin = -> Origin1164
  Placement = pos=(0,0,0) rot=(0,0.707107,0.707107;3.14159rad)
  Tip = -> Pocket962
FEATURE [PartDesign::Thickness] Thickness005
  Base = -> Pad1236 [Face7,Face8,Face2]
  BaseFeature = -> Pad1236
  Join = 0
  Mode = 0
  Value = 2
FEATURE [PartDesign::Pad] Pad1234  label="Front Expansion004"
  BaseFeature = -> Thickness005
  Length = 23.75
  Length2 = 100
  Profile = -> Thickness005 [Face6]
  Type = 0
FEATURE [PartDesign::Pad] Pad1230  label="Rear Expansion004"
  BaseFeature = -> Pad1234
  Length = 23.75
  Length2 = 100
  Profile = -> Pad1234 [Face5]
  Type = 0
FEATURE [Sketcher::SketchObject] Sketch2717
  MapMode = 5
  Placement = pos=(0,-9.2e-15,42) rot=(0,0,1;0rad)
  Support = -> [Pad1230]
  sketch-geometry (16):
    g0: LineSegment StartX=-2 StartY=0 StartZ=0 EndX=40 EndY=0 EndZ=0
    g1: LineSegment StartX=40 StartY=0 StartZ=0 EndX=40 EndY=-23.75 EndZ=0
    g2: LineSegment StartX=40 StartY=-23.75 StartZ=0 EndX=-2 EndY=-23.75 EndZ=0
    g3: LineSegment StartX=-2 StartY=-23.75 StartZ=0 EndX=-2 EndY=0 EndZ=0
    g4: LineSegment StartX=112 StartY=0 StartZ=0 EndX=70 EndY=0 EndZ=0
    g5: LineSegment StartX=70 StartY=0 StartZ=0 EndX=70 EndY=-23.75 EndZ=0
    g6: LineSegment StartX=70 StartY=-23.75 StartZ=0 EndX=112 EndY=-23.75 EndZ=0
    g7: LineSegment StartX=112 StartY=-23.75 StartZ=0 EndX=112 EndY=0 EndZ=0
    g8: LineSegment StartX=-2 StartY=160 StartZ=0 EndX=40 EndY=160 EndZ=0
    g9: LineSegment StartX=40 StartY=160 StartZ=0 EndX=40 EndY=183.75 EndZ=0
    g10: LineSegment StartX=40 StartY=183.75 StartZ=0 EndX=-2 EndY=183.75 EndZ=0
    g11: LineSegment StartX=-2 StartY=183.75 StartZ=0 EndX=-2 EndY=160 EndZ=0
    g12: LineSegment StartX=112 StartY=183.75 StartZ=0 EndX=70 EndY=183.75 EndZ=0
    g13: LineSegment StartX=70 StartY=183.75 StartZ=0 EndX=70 EndY=160 EndZ=0
    g14: LineSegment StartX=70 StartY=160 StartZ=0 EndX=112 EndY=160 EndZ=0
    g15: LineSegment StartX=112 StartY=160 StartZ=0 EndX=112 EndY=183.75 EndZ=0
  constraints (48):
    c: Coincident(g0,g1)
    c: Coincident(g1,g2)
    c: Coincident(g2,g3)
    c: Coincident(g3,g0)
    c: Horizontal(g0)
    c: Horizontal(g2)
    c: Vertical(g1)
    c: Vertical(g3)
    c: PointOnObject(g0,g-1)
    c: Coincident(g4,g5)
    c: Coincident(g5,g6)
    c: Coincident(g6,g7)
    c: Coincident(g7,g4)
    c: Horizontal(g4)
    c: Horizontal(g6)
    c: Vertical(g5)
    c: Vertical(g7)
    c: Coincident(g8,g9)
    c: Coincident(g9,g10)
    c: Coincident(g10,g11)
    c: Coincident(g11,g8)
    c: Horizontal(g8)
    c: Horizontal(g10)
    c: Vertical(g9)
    c: Vertical(g11)
    c: Coincident(g12,g13)
    c: Coincident(g13,g14)
    c: Coincident(g14,g15)
    c: Coincident(g15,g12)
    c: Horizontal(g12)
    c: Horizontal(g14)
    c: Vertical(g13)
    c: Vertical(g15)
    c: Horizontal(g9,g12)
    c: Equal(g9,g13)
    c: Equal(g10,g12)
    c: Equal(g0,g8)
    c: Equal(g4,g14)
    c: Horizontal(g0,g4)
    c: Equal(g5,g1)
    c: DistanceX(g0,g4) = 30
    c: DistanceX(g0,g0) = 42
    c: DistanceY(g3,g3) = 23.75
    c: DistanceX(g0,g-1) = 2
    c: Vertical(g0,g8)
    c: Vertical(g13,g4)
    c: DistanceY(g0,g8) = 160
    c: Equal(g9,g1)
FEATURE [PartDesign::Pocket] Pocket955  label="Shoulders003"
  BaseFeature = -> Pad1230
  Length = 42
  Length2 = 100
  Profile = -> Sketch2717
  Type = 0
FEATURE [Sketcher::SketchObject] Sketch2715
  MapMode = 5
  Placement = pos=(112,0,0) rot=(0.57735,0.57735,0.57735;2.0944rad)
  Support = -> [Pocket955]
  sketch-geometry (6):
    g0: LineSegment StartX=0 StartY=-5 StartZ=0 EndX=-2e-16 EndY=12 EndZ=0
    g1: LineSegment StartX=-2e-16 StartY=12 StartZ=0 EndX=75 EndY=12 EndZ=0
    g2: LineSegment StartX=75 StartY=12 StartZ=0 EndX=105 EndY=0 EndZ=0
    g3: LineSegment StartX=105 StartY=0 StartZ=0 EndX=160 EndY=0 EndZ=0
    g4: LineSegment StartX=160 StartY=0 StartZ=0 EndX=160 EndY=-5 EndZ=0
    g5: LineSegment StartX=160 StartY=-5 StartZ=0 EndX=0 EndY=-5 EndZ=0
  constraints (18):
    c: PointOnObject(g0,g-2)
    c: Coincident(g0,g1)
    c: Horizontal(g1)
    c: Coincident(g1,g2)
    c: PointOnObject(g2,g-1)
    c: Coincident(g2,g3)
    c: Horizontal(g3)
    c: Coincident(g3,g4)
    c: Vertical(g4)
    c: Coincident(g4,g5)
    c: PointOnObject(g5,g-2)
    c: Horizontal(g5)
    c: Coincident(g0,g5)
    c: DistanceX(g1,g2) = 30
    c: DistanceX(g5,g5) = 160
    c: DistanceX(g1,g1) = 75
    c: DistanceY(g-1,g0) = 12
    c: DistanceY(g4,g4) = 5
FEATURE [PartDesign::Pocket] Pocket954  label="Side Detailing003"
  BaseFeature = -> Pocket955
  Length = 114
  Length2 = 100
  Profile = -> Sketch2715
  Type = 0
FEATURE [Sketcher::SketchObject] Sketch2714
  MapMode = 5
  Placement = pos=(0,-9.2e-15,42) rot=(0,0,1;0rad)
  Support = -> [Pocket954]
  sketch-geometry (4):
    g0: Circle CenterX=50 CenterY=-18.75 CenterZ=0 NormalX=0 NormalY=0 NormalZ=1 AngleXU=0 Radius=1.6
    g1: Circle CenterX=60 CenterY=-18.75 CenterZ=0 NormalX=0 NormalY=0 NormalZ=1 AngleXU=0 Radius=1.6
    g2: Circle CenterX=50 CenterY=178.75 CenterZ=0 NormalX=0 NormalY=0 NormalZ=1 AngleXU=0 Radius=1.6
    g3: Circle CenterX=60 CenterY=178.75 CenterZ=0 NormalX=0 NormalY=0 NormalZ=1 AngleXU=0 Radius=1.6
  constraints (12):
    c: DistanceX(g2,g3) = 10
    c: Equal(g2,g3)
    c: Equal(g3,g0)
    c: Equal(g0,g1)
    c: Horizontal(g2,g3)
    c: Horizontal(g0,g1)
    c: Vertical(g1,g3)
    c: Vertical(g0,g2)
    c: DistanceY(g0,g-1) = 18.75
    c: DistanceX(g-1,g0) = 50
    c: DistanceY(g-1,g2) = 178.75
    c: Radius(g3) = 1.6
FEATURE [PartDesign::Pocket] Pocket964  label="Screwholes015"
  BaseFeature = -> Pocket954
  Length = 2
  Length2 = 100
  Profile = -> Sketch2714
  Type = 0
FEATURE [PartDesign::Fillet] Fillet288  label="Round Corners004"
  Base = -> Pocket964 [Edge35,Edge66,Edge48,Edge12,Edge18,Edge44,Edge25,Edge76,Edge57,Edge60,Edge45,Edge9]
  BaseFeature = -> Pocket964
  Radius = 5
FEATURE [PartDesign::Fillet] Fillet285  label="Round Side Details004"
  Base = -> Fillet288 [Edge10,Edge16,Edge131,Edge132]
  BaseFeature = -> Fillet288
  Radius = 20
FEATURE [PartDesign::Pad] Pad1229  label="Screwpads003"
  BaseFeature = -> Fillet285
  Length = 5.5
  Length2 = 5.5
  Profile = -> Sketch2719
  Type = 4
FEATURE [PartDesign::Fillet] Fillet287  label="Smooth Screwpad Edges004"
  Base = -> Pad1229 [Edge169,Edge130,Edge126,Edge122,Edge118,Edge29,Edge27,Edge97,Edge65,Edge61,Edge63,Edge59]
  BaseFeature = -> Pad1229
  Radius = 1
FEATURE [PartDesign::Fillet] Fillet286  label="Smooth Screwpad Edges Side Details004"
  Base = -> Fillet287 [Edge207,Edge22]
  BaseFeature = -> Fillet287
  Radius = 0.2
FEATURE [Sketcher::SketchObject] Sketch2720
  MapMode = 5
  Placement = pos=(0,114.35,0) rot=(0,0.707107,0.707107;3.14159rad)
  Support = -> [Fillet286]
  sketch-geometry (4):
    g0: Circle CenterX=-106.75 CenterY=18.25 CenterZ=0 NormalX=0 NormalY=0 NormalZ=1 AngleXU=0 Radius=1.6
    g1: Circle CenterX=-70 CenterY=36.75 CenterZ=0 NormalX=0 NormalY=0 NormalZ=1 AngleXU=0 Radius=1.6
    g2: Circle CenterX=-40 CenterY=36.75 CenterZ=0 NormalX=0 NormalY=0 NormalZ=1 AngleXU=0 Radius=1.6
    g3: Circle CenterX=-3.25 CenterY=18.25 CenterZ=0 NormalX=0 NormalY=0 NormalZ=1 AngleXU=0 Radius=1.6
  constraints (12):
    c: Equal(g0,g1)
    c: Equal(g1,g2)
    c: Equal(g2,g3)
    c: Radius(g3) = 1.6
    c: Horizontal(g1,g2)
    c: Horizontal(g0,g3)
    c: DistanceX(g3,g-1) = 3.25
    c: DistanceY(g-1,g3) = 18.25
    c: DistanceX(g0,g3) = 103.5
    c: DistanceX(g1,g2) = 30
    c: DistanceY(g-1,g2) = 36.75
    c: DistanceX(g2,g-1) = 40
FEATURE [PartDesign::Pocket] Pocket966  label="Screwholes Connection004"
  BaseFeature = -> Fillet286
  Length = 11
  Length2 = 100
  Profile = -> Sketch2720
  Type = 0
FEATURE [Sketcher::SketchObject] Sketch2718
  MapMode = 5
  Placement = pos=(0,114.35,0) rot=(0,0.707107,0.707107;3.14159rad)
  Support = -> [Pocket966]
  sketch-geometry (4):
    g0: Circle CenterX=-106.75 CenterY=18.25 CenterZ=0 NormalX=0 NormalY=0 NormalZ=1 AngleXU=0 Radius=2.85
    g1: Circle CenterX=-70 CenterY=36.75 CenterZ=0 NormalX=0 NormalY=0 NormalZ=1 AngleXU=0 Radius=2.85
    g2: Circle CenterX=-40 CenterY=36.75 CenterZ=0 NormalX=0 NormalY=0 NormalZ=1 AngleXU=0 Radius=2.85
    g3: Circle CenterX=-3.25 CenterY=18.25 CenterZ=0 NormalX=0 NormalY=0 NormalZ=1 AngleXU=0 Radius=2.85
  constraints (12):
    c: Equal(g3,g2)
    c: Equal(g2,g1)
    c: Equal(g1,g0)
    c: Radius(g3) = 2.85
    c: DistanceX(g3,g-1) = 3.25
    c: DistanceY(g-1,g3) = 18.25
    c: Horizontal(g3,g0)
    c: DistanceX(g0,g3) = 103.5
    c: DistanceX(g1,g2) = 30
    c: DistanceY(g-1,g2) = 36.75
    c: DistanceX(g2,g-1) = 40
    c: Horizontal(g1,g2)
FEATURE [PartDesign::Pocket] Pocket963  label="Screwheads Connection004"
  BaseFeature = -> Pocket966
  Length = 3
  Length2 = 100
  Profile = -> Sketch2718
  Type = 0
FEATURE [Sketcher::SketchObject] Sketch2721
  MapMode = 5
  Placement = pos=(0,103.35,0) rot=(1,0,0;1.5708rad)
  Support = -> [Pocket963]
  sketch-geometry (28):
    g0: LineSegment StartX=3.25 StartY=21.5409 StartZ=0 EndX=0.4 EndY=19.8954 EndZ=0
    g1: LineSegment StartX=0.4 StartY=19.8954 StartZ=0 EndX=0.4 EndY=16.6046 EndZ=0
    g2: LineSegment StartX=0.4 StartY=16.6046 StartZ=0 EndX=3.25 EndY=14.9591 EndZ=0
    g3: LineSegment StartX=3.25 StartY=14.9591 StartZ=0 EndX=6.1 EndY=16.6046 EndZ=0
    g4: LineSegment StartX=6.1 StartY=16.6046 StartZ=0 EndX=6.1 EndY=19.8954 EndZ=0
    g5: LineSegment StartX=6.1 StartY=19.8954 StartZ=0 EndX=3.25 EndY=21.5409 EndZ=0
    g6: Circle [constr] CenterX=3.25 CenterY=18.25 CenterZ=0 NormalX=0 NormalY=0 NormalZ=1 AngleXU=0 Radius=3.2909
    g7: LineSegment StartX=42.85 StartY=38.3954 StartZ=0 EndX=40 EndY=40.0409 EndZ=0
    g8: LineSegment StartX=40 StartY=40.0409 StartZ=0 EndX=37.15 EndY=38.3954 EndZ=0
    g9: LineSegment StartX=37.15 StartY=38.3954 StartZ=0 EndX=37.15 EndY=35.1046 EndZ=0
    g10: LineSegment StartX=37.15 StartY=35.1046 StartZ=0 EndX=40 EndY=33.4591 EndZ=0
    g11: LineSegment StartX=40 StartY=33.4591 StartZ=0 EndX=42.85 EndY=35.1046 EndZ=0
    g12: LineSegment StartX=42.85 StartY=35.1046 StartZ=0 EndX=42.85 EndY=38.3954 EndZ=0
    g13: Circle [constr] CenterX=40 CenterY=36.75 CenterZ=0 NormalX=0 NormalY=0 NormalZ=1 AngleXU=0 Radius=3.2909
    g14: LineSegment StartX=72.85 StartY=38.3954 StartZ=0 EndX=70 EndY=40.0409 EndZ=0
    g15: LineSegment StartX=70 StartY=40.0409 StartZ=0 EndX=67.15 EndY=38.3954 EndZ=0
    g16: LineSegment StartX=67.15 StartY=38.3954 StartZ=0 EndX=67.15 EndY=35.1046 EndZ=0
    g17: LineSegment StartX=67.15 StartY=35.1046 StartZ=0 EndX=70 EndY=33.4591 EndZ=0
    g18: LineSegment StartX=70 StartY=33.4591 StartZ=0 EndX=72.85 EndY=35.1046 EndZ=0
    g19: LineSegment StartX=72.85 StartY=35.1046 StartZ=0 EndX=72.85 EndY=38.3954 EndZ=0
    g20: Circle [constr] CenterX=70 CenterY=36.75 CenterZ=0 NormalX=0 NormalY=0 NormalZ=1 AngleXU=0 Radius=3.2909
    g21: LineSegment StartX=106.75 StartY=21.5409 StartZ=0 EndX=103.9 EndY=19.8954 EndZ=0
    g22: LineSegment StartX=103.9 StartY=19.8954 StartZ=0 EndX=103.9 EndY=16.6046 EndZ=0
    g23: LineSegment StartX=103.9 StartY=16.6046 StartZ=0 EndX=106.75 EndY=14.9591 EndZ=0
    g24: LineSegment StartX=106.75 StartY=14.9591 StartZ=0 EndX=109.6 EndY=16.6046 EndZ=0
    g25: LineSegment StartX=109.6 StartY=16.6046 StartZ=0 EndX=109.6 EndY=19.8954 EndZ=0
    g26: LineSegment StartX=109.6 StartY=19.8954 StartZ=0 EndX=106.75 EndY=21.5409 EndZ=0
    g27: Circle [constr] CenterX=106.75 CenterY=18.25 CenterZ=0 NormalX=0 NormalY=0 NormalZ=1 AngleXU=0 Radius=3.2909
  constraints (68):
    c: Coincident(g0,g1)
    c: Coincident(g1,g2)
    c: Coincident(g2,g3)
    c: Coincident(g3,g4)
    c: Coincident(g4,g5)
    c: Coincident(g5,g0)
    c: Equal(g0, g1-g5) x5
    c: PointOnObject(g0,g6)
    c: PointOnObject(g1,g6)
    c: PointOnObject(g2,g6)
    c: PointOnObject(g3,g6)
    c: PointOnObject(g4,g6)
    c: PointOnObject(g5,g6)
    c: Coincident(g7,g8)
    c: Coincident(g8,g9)
    c: Coincident(g9,g10)
    c: Coincident(g10,g11)
    c: Coincident(g11,g12)
    c: Coincident(g12,g7)
    c: Equal(g7, g8-g12) x5
    c: PointOnObject(g7,g13)
    c: PointOnObject(g8,g13)
    c: PointOnObject(g9,g13)
    c: PointOnObject(g10,g13)
    c: PointOnObject(g11,g13)
    c: PointOnObject(g12,g13)
    c: Coincident(g14,g15)
    c: Coincident(g15,g16)
    c: Coincident(g16,g17)
    c: Coincident(g17,g18)
    c: Coincident(g18,g19)
    c: Coincident(g19,g14)
    c: Equal(g14, g15-g19) x5
    c: PointOnObject(g14,g20)
    c: PointOnObject(g15,g20)
    c: PointOnObject(g16,g20)
    c: PointOnObject(g17,g20)
    c: PointOnObject(g18,g20)
    c: PointOnObject(g19,g20)
    c: Coincident(g21,g22)
    c: Coincident(g22,g23)
    c: Coincident(g23,g24)
    c: Coincident(g24,g25)
    c: Coincident(g25,g26)
    c: Coincident(g26,g21)
    c: Equal(g21, g22-g26) x5
    c: PointOnObject(g21,g27)
    c: PointOnObject(g22,g27)
    c: PointOnObject(g23,g27)
    c: PointOnObject(g24,g27)
    c: PointOnObject(g25,g27)
    c: PointOnObject(g26,g27)
    c: Vertical(g12)
    c: Vertical(g16)
    c: Vertical(g4)
    c: Vertical(g22)
    c: Equal(g27,g20)
    c: Equal(g20,g13)
    c: Equal(g13,g6)
    c: DistanceX(g21,g25) = 5.7
    c: DistanceX(g-1,g6) = 3.25
    c: DistanceY(g-1,g6) = 18.25
    c: DistanceX(g6,g27) = 103.5
    c: Horizontal(g27,g6)
    c: Horizontal(g13,g20)
    c: DistanceX(g13,g20) = 30
    c: DistanceY(g-1,g13) = 36.75
    c: DistanceX(g-1,g13) = 40
FEATURE [PartDesign::Pocket] Pocket961  label="Nutholes Connection004"
  BaseFeature = -> Pocket963
  Length = 2.5
  Length2 = 100
  Profile = -> Sketch2721
  Type = 0
FEATURE [Sketcher::SketchObject] Sketch2722
  MapMode = 5
  Placement = pos=(112,0,0) rot=(0.57735,0.57735,0.57735;2.0944rad)
  Support = -> [Pocket961]
  sketch-geometry (4):
    g0: LineSegment StartX=188.85 StartY=0 StartZ=0 EndX=108.85 EndY=0 EndZ=0
    g1: LineSegment StartX=108.85 StartY=0 StartZ=0 EndX=108.85 EndY=42 EndZ=0
    g2: LineSegment StartX=108.85 StartY=42 StartZ=0 EndX=188.85 EndY=42 EndZ=0
    g3: LineSegment StartX=188.85 StartY=42 StartZ=0 EndX=188.85 EndY=0 EndZ=0
  constraints (12):
    c: Coincident(g0,g1)
    c: Coincident(g1,g2)
    c: Coincident(g2,g3)
    c: Coincident(g3,g0)
    c: Horizontal(g0)
    c: Horizontal(g2)
    c: Vertical(g1)
    c: Vertical(g3)
    c: PointOnObject(g0,g-1)
    c: DistanceX(g-1,g0) = 108.85
    c: DistanceY(g3,g3) = 42
    c: DistanceX(g2,g2) = 80
FEATURE [PartDesign::Pocket] Pocket965  label="Remove Rear001"
  BaseFeature = -> Pocket961
  Length = 114
  Length2 = 100
  Profile = -> Sketch2722
  Type = 0
FEATURE [PartDesign::Body] Body820  label="Bottom_Cover_Split_Front"
  Group = -> [Sketch2716,Pad1236,Thickness005,Pad1234,Pad1230,Sketch2717,Pocket955,Sketch2715,Pocket954,Sketch2714,Pocket964,Fillet288,Fillet285,Sketch2719,Pad1229,Fillet287,Fillet286,Sketch2720,Pocket966,Sketch2718,Pocket963,Sketch2721,Pocket961,Sketch2722,Pocket965]
  Origin = -> Origin1163
  Placement = pos=(0,0,0) rot=(0,0.707107,0.707107;3.14159rad)
  Tip = -> Pocket965
FEATURE [Sketcher::SketchObject] Sketch2740
  MapMode = 5
  Support = -> [XY_Plane1170]
  sketch-geometry (8):
    g0: LineSegment StartX=0 StartY=3.17543 StartZ=0 EndX=-2.75 EndY=1.58771 EndZ=0
    g1: LineSegment StartX=-2.75 StartY=1.58771 StartZ=0 EndX=-2.75 EndY=-1.58771 EndZ=0
    g2: LineSegment StartX=-2.75 StartY=-1.58771 StartZ=0 EndX=0 EndY=-3.17543 EndZ=0
    g3: LineSegment StartX=0 StartY=-3.17543 StartZ=0 EndX=2.75 EndY=-1.58771 EndZ=0
    g4: LineSegment StartX=2.75 StartY=-1.58771 StartZ=0 EndX=2.75 EndY=1.58771 EndZ=0
    g5: LineSegment StartX=2.75 StartY=1.58771 StartZ=0 EndX=0 EndY=3.17543 EndZ=0
    g6: Circle [constr] CenterX=0 CenterY=0 CenterZ=0 NormalX=0 NormalY=0 NormalZ=1 AngleXU=0 Radius=3.17543
    g7: Circle CenterX=0 CenterY=0 CenterZ=0 NormalX=0 NormalY=0 NormalZ=1 AngleXU=0 Radius=1.5
  constraints (18):
    c: Coincident(g0,g1)
    c: Coincident(g1,g2)
    c: Coincident(g2,g3)
    c: Coincident(g3,g4)
    c: Coincident(g4,g5)
    c: Coincident(g5,g0)
    c: Equal(g0, g1-g5) x5
    c: PointOnObject(g0,g6)
    c: PointOnObject(g1,g6)
    c: PointOnObject(g2,g6)
    c: PointOnObject(g3,g6)
    c: PointOnObject(g4,g6)
    c: PointOnObject(g5,g6)
    c: Coincident(g6,g-1)
    c: PointOnObject(g5,g-2)
    c: DistanceX(g0,g4) = 5.5
    c: Coincident(g7,g-1)
    c: Radius(g7) = 1.5
FEATURE [PartDesign::Pad] Pad1239  label="M3 Nut Primitive253"
  Length = 1.2
  Length2 = 1.2
  Profile = -> Sketch2740
  Type = 4
FEATURE [Sketcher::SketchObject] Sketch2741
  MapMode = 5
  Placement = pos=(0,0,3) rot=(0,0,1;0rad)
  Support = -> [Pad1237]
  sketch-geometry (1):
    g0: Circle CenterX=0 CenterY=0 CenterZ=0 NormalX=0 NormalY=0 NormalZ=1 AngleXU=0 Radius=1.5
  constraints (2):
    c: Coincident(g0,g-1)
    c: Radius(g0) = 1.5
FEATURE [PartDesign::Pad] Pad1245  label="M3x8 Thread205"
  BaseFeature = -> Pad1237
  Length = 8
  Length2 = 100
  Profile = -> Sketch2741
  Type = 0
FEATURE [Sketcher::SketchObject] Sketch2735
  MapMode = 5
  Placement = pos=(0,0,0) rot=(1,0,0;3.14159rad)
  Support = -> [Pad1245]
  sketch-geometry (7):
    g0: LineSegment StartX=1.275 StartY=0.736122 StartZ=0 EndX=0 EndY=1.47224 EndZ=0
    g1: LineSegment StartX=0 StartY=1.47224 StartZ=0 EndX=-1.275 EndY=0.736122 EndZ=0
    g2: LineSegment StartX=-1.275 StartY=0.736122 StartZ=0 EndX=-1.275 EndY=-0.736122 EndZ=0
    g3: LineSegment StartX=-1.275 StartY=-0.736122 StartZ=0 EndX=1.34766e-11 EndY=-1.47224 EndZ=0
    g4: LineSegment StartX=1.34766e-11 StartY=-1.47224 StartZ=0 EndX=1.275 EndY=-0.736122 EndZ=0
    g5: LineSegment StartX=1.275 StartY=-0.736122 StartZ=0 EndX=1.275 EndY=0.736122 EndZ=0
    g6: Circle [constr] CenterX=0 CenterY=0 CenterZ=0 NormalX=0 NormalY=0 NormalZ=1 AngleXU=0 Radius=1.47224
  constraints (16):
    c: Coincident(g0,g1)
    c: Coincident(g1,g2)
    c: Coincident(g2,g3)
    c: Coincident(g3,g4)
    c: Coincident(g4,g5)
    c: Coincident(g5,g0)
    c: Equal(g0, g1-g5) x5
    c: PointOnObject(g0,g6)
    c: PointOnObject(g1,g6)
    c: PointOnObject(g2,g6)
    c: PointOnObject(g3,g6)
    c: PointOnObject(g4,g6)
    c: PointOnObject(g5,g6)
    c: Coincident(g6,g-1)
    c: PointOnObject(g0,g-2)
    c: DistanceX(g1,g0) = 2.55
FEATURE [PartDesign::Pocket] Pocket967  label="M3x8 Wrench203"
  BaseFeature = -> Pad1245
  Length = 1.3
  Length2 = 100
  Profile = -> Sketch2735
  Type = 0
FEATURE [PartDesign::Chamfer] Chamfer623  label="M3x8 Smooth202"
  Base = -> Pocket967 [Face11,Edge2,Edge24,Edge3]
  BaseFeature = -> Pocket967
  Size = 0.2
FEATURE [PartDesign::Body] Body824  label="M3x172"
  Group = -> [Sketch2736,Pad1237,Sketch2741,Pad1245,Sketch2735,Pocket967,Chamfer623]
  Origin = -> Origin1166
  Placement = pos=(36.75,13.5,0) rot=(0,0,1;0rad)
  Tip = -> Chamfer623
FEATURE [Sketcher::SketchObject] Sketch2743
  MapMode = 5
  Support = -> [XY_Plane1164]
  sketch-geometry (1):
    g0: Circle CenterX=0 CenterY=0 CenterZ=0 NormalX=0 NormalY=0 NormalZ=1 AngleXU=0 Radius=2.75
  constraints (2):
    c: Coincident(g0,g-1)
    c: Radius(g0) = 2.75
FEATURE [PartDesign::Pad] Pad1235  label="M3x8 Head203"
  Length = 3
  Length2 = 100
  Profile = -> Sketch2743
  Type = 0
FEATURE [Sketcher::SketchObject] Sketch2742
  MapMode = 5
  Placement = pos=(0,0,3) rot=(0,0,1;0rad)
  Support = -> [Pad1235]
  sketch-geometry (1):
    g0: Circle CenterX=0 CenterY=0 CenterZ=0 NormalX=0 NormalY=0 NormalZ=1 AngleXU=0 Radius=1.5
  constraints (2):
    c: Coincident(g0,g-1)
    c: Radius(g0) = 1.5
FEATURE [PartDesign::Pad] Pad1244  label="M3x8 Thread204"
  BaseFeature = -> Pad1235
  Length = 8
  Length2 = 100
  Profile = -> Sketch2742
  Type = 0
FEATURE [Sketcher::SketchObject] Sketch2734
  MapMode = 5
  Placement = pos=(0,0,0) rot=(1,0,0;3.14159rad)
  Support = -> [Pad1244]
  sketch-geometry (7):
    g0: LineSegment StartX=1.275 StartY=0.736122 StartZ=0 EndX=0 EndY=1.47224 EndZ=0
    g1: LineSegment StartX=0 StartY=1.47224 StartZ=0 EndX=-1.275 EndY=0.736122 EndZ=0
    g2: LineSegment StartX=-1.275 StartY=0.736122 StartZ=0 EndX=-1.275 EndY=-0.736122 EndZ=0
    g3: LineSegment StartX=-1.275 StartY=-0.736122 StartZ=0 EndX=1.34766e-11 EndY=-1.47224 EndZ=0
    g4: LineSegment StartX=1.34766e-11 StartY=-1.47224 StartZ=0 EndX=1.275 EndY=-0.736122 EndZ=0
    g5: LineSegment StartX=1.275 StartY=-0.736122 StartZ=0 EndX=1.275 EndY=0.736122 EndZ=0
    g6: Circle [constr] CenterX=0 CenterY=0 CenterZ=0 NormalX=0 NormalY=0 NormalZ=1 AngleXU=0 Radius=1.47224
  constraints (16):
    c: Coincident(g0,g1)
    c: Coincident(g1,g2)
    c: Coincident(g2,g3)
    c: Coincident(g3,g4)
    c: Coincident(g4,g5)
    c: Coincident(g5,g0)
    c: Equal(g0, g1-g5) x5
    c: PointOnObject(g0,g6)
    c: PointOnObject(g1,g6)
    c: PointOnObject(g2,g6)
    c: PointOnObject(g3,g6)
    c: PointOnObject(g4,g6)
    c: PointOnObject(g5,g6)
    c: Coincident(g6,g-1)
    c: PointOnObject(g0,g-2)
    c: DistanceX(g1,g0) = 2.55
FEATURE [PartDesign::Pocket] Pocket968  label="M3x8 Wrench204"
  BaseFeature = -> Pad1244
  Length = 1.3
  Length2 = 100
  Profile = -> Sketch2734
  Type = 0
FEATURE [PartDesign::Chamfer] Chamfer628  label="M3x8 Smooth205"
  Base = -> Pocket968 [Face11,Edge2,Edge24,Edge3]
  BaseFeature = -> Pocket968
  Size = 0.2
FEATURE [PartDesign::Body] Body826  label="M3x174"
  Group = -> [Sketch2743,Pad1235,Sketch2742,Pad1244,Sketch2734,Pocket968,Chamfer628]
  Origin = -> Origin1173
  Placement = pos=(0,-5,0) rot=(0,0,1;0rad)
  Tip = -> Chamfer628
FEATURE [Sketcher::SketchObject] Sketch2745
  MapMode = 5
  Support = -> [XY_Plane1169]
  sketch-geometry (1):
    g0: Circle CenterX=0 CenterY=0 CenterZ=0 NormalX=0 NormalY=0 NormalZ=1 AngleXU=0 Radius=2.75
  constraints (2):
    c: Coincident(g0,g-1)
    c: Radius(g0) = 2.75
FEATURE [PartDesign::Pad] Pad1238  label="M3x8 Head205"
  Length = 3
  Length2 = 100
  Profile = -> Sketch2745
  Type = 0
FEATURE [Sketcher::SketchObject] Sketch2746
  MapMode = 5
  Placement = pos=(0,0,3) rot=(0,0,1;0rad)
  Support = -> [Pad1238]
  sketch-geometry (1):
    g0: Circle CenterX=0 CenterY=0 CenterZ=0 NormalX=0 NormalY=0 NormalZ=1 AngleXU=0 Radius=1.5
  constraints (2):
    c: Coincident(g0,g-1)
    c: Radius(g0) = 1.5
FEATURE [PartDesign::Pad] Pad1243  label="M3x8 Thread203"
  BaseFeature = -> Pad1238
  Length = 8
  Length2 = 100
  Profile = -> Sketch2746
  Type = 0
FEATURE [Sketcher::SketchObject] Sketch2738
  MapMode = 5
  Placement = pos=(0,0,0) rot=(1,0,0;3.14159rad)
  Support = -> [Pad1243]
  sketch-geometry (7):
    g0: LineSegment StartX=1.275 StartY=0.736122 StartZ=0 EndX=0 EndY=1.47224 EndZ=0
    g1: LineSegment StartX=0 StartY=1.47224 StartZ=0 EndX=-1.275 EndY=0.736122 EndZ=0
    g2: LineSegment StartX=-1.275 StartY=0.736122 StartZ=0 EndX=-1.275 EndY=-0.736122 EndZ=0
    g3: LineSegment StartX=-1.275 StartY=-0.736122 StartZ=0 EndX=1.34766e-11 EndY=-1.47224 EndZ=0
    g4: LineSegment StartX=1.34766e-11 StartY=-1.47224 StartZ=0 EndX=1.275 EndY=-0.736122 EndZ=0
    g5: LineSegment StartX=1.275 StartY=-0.736122 StartZ=0 EndX=1.275 EndY=0.736122 EndZ=0
    g6: Circle [constr] CenterX=0 CenterY=0 CenterZ=0 NormalX=0 NormalY=0 NormalZ=1 AngleXU=0 Radius=1.47224
  constraints (16):
    c: Coincident(g0,g1)
    c: Coincident(g1,g2)
    c: Coincident(g2,g3)
    c: Coincident(g3,g4)
    c: Coincident(g4,g5)
    c: Coincident(g5,g0)
    c: Equal(g0, g1-g5) x5
    c: PointOnObject(g0,g6)
    c: PointOnObject(g1,g6)
    c: PointOnObject(g2,g6)
    c: PointOnObject(g3,g6)
    c: PointOnObject(g4,g6)
    c: PointOnObject(g5,g6)
    c: Coincident(g6,g-1)
    c: PointOnObject(g0,g-2)
    c: DistanceX(g1,g0) = 2.55
FEATURE [PartDesign::Pocket] Pocket969  label="M3x8 Wrench205"
  BaseFeature = -> Pad1243
  Length = 1.3
  Length2 = 100
  Profile = -> Sketch2738
  Type = 0
FEATURE [PartDesign::Chamfer] Chamfer624  label="M3x8 Smooth203"
  Base = -> Pocket969 [Face11,Edge2,Edge24,Edge3]
  BaseFeature = -> Pocket969
  Size = 0.2
FEATURE [PartDesign::Body] Body825  label="M3x173"
  Group = -> [Sketch2745,Pad1238,Sketch2746,Pad1243,Sketch2738,Pocket969,Chamfer624]
  Origin = -> Origin1172
  Placement = pos=(66.75,13.5,0) rot=(0,0,1;0rad)
  Tip = -> Chamfer624
FEATURE [Sketcher::SketchObject] Sketch2747
  MapMode = 5
  Support = -> [XY_Plane1167]
  sketch-geometry (1):
    g0: Circle CenterX=0 CenterY=0 CenterZ=0 NormalX=0 NormalY=0 NormalZ=1 AngleXU=0 Radius=2.75
  constraints (2):
    c: Coincident(g0,g-1)
    c: Radius(g0) = 2.75
FEATURE [PartDesign::Pad] Pad1246  label="M3x8 Head206"
  Length = 3
  Length2 = 100
  Profile = -> Sketch2747
  Type = 0
FEATURE [Sketcher::SketchObject] Sketch2744
  MapMode = 5
  Placement = pos=(0,0,3) rot=(0,0,1;0rad)
  Support = -> [Pad1246]
  sketch-geometry (1):
    g0: Circle CenterX=0 CenterY=0 CenterZ=0 NormalX=0 NormalY=0 NormalZ=1 AngleXU=0 Radius=1.5
  constraints (2):
    c: Coincident(g0,g-1)
    c: Radius(g0) = 1.5
FEATURE [PartDesign::Pad] Pad1247  label="M3x8 Thread206"
  BaseFeature = -> Pad1246
  Length = 8
  Length2 = 100
  Profile = -> Sketch2744
  Type = 0
FEATURE [Sketcher::SketchObject] Sketch2748
  MapMode = 5
  Support = -> [XY_Plane1172]
  sketch-geometry (8):
    g0: LineSegment StartX=0 StartY=3.17543 StartZ=0 EndX=-2.75 EndY=1.58771 EndZ=0
    g1: LineSegment StartX=-2.75 StartY=1.58771 StartZ=0 EndX=-2.75 EndY=-1.58771 EndZ=0
    g2: LineSegment StartX=-2.75 StartY=-1.58771 StartZ=0 EndX=0 EndY=-3.17543 EndZ=0
    g3: LineSegment StartX=0 StartY=-3.17543 StartZ=0 EndX=2.75 EndY=-1.58771 EndZ=0
    g4: LineSegment StartX=2.75 StartY=-1.58771 StartZ=0 EndX=2.75 EndY=1.58771 EndZ=0
    g5: LineSegment StartX=2.75 StartY=1.58771 StartZ=0 EndX=0 EndY=3.17543 EndZ=0
    g6: Circle [constr] CenterX=0 CenterY=0 CenterZ=0 NormalX=0 NormalY=0 NormalZ=1 AngleXU=0 Radius=3.17543
    g7: Circle CenterX=0 CenterY=0 CenterZ=0 NormalX=0 NormalY=0 NormalZ=1 AngleXU=0 Radius=1.5
  constraints (18):
    c: Coincident(g0,g1)
    c: Coincident(g1,g2)
    c: Coincident(g2,g3)
    c: Coincident(g3,g4)
    c: Coincident(g4,g5)
    c: Coincident(g5,g0)
    c: Equal(g0, g1-g5) x5
    c: PointOnObject(g0,g6)
    c: PointOnObject(g1,g6)
    c: PointOnObject(g2,g6)
    c: PointOnObject(g3,g6)
    c: PointOnObject(g4,g6)
    c: PointOnObject(g5,g6)
    c: Coincident(g6,g-1)
    c: PointOnObject(g5,g-2)
    c: DistanceX(g0,g4) = 5.5
    c: Coincident(g7,g-1)
    c: Radius(g7) = 1.5
FEATURE [PartDesign::Pad] Pad1241  label="M3 Nut Primitive255"
  Length = 1.2
  Length2 = 1.2
  Profile = -> Sketch2748
  Type = 4
FEATURE [Sketcher::SketchObject] Sketch2749
  ExternalGeometry = -> [Pad1241]
  MapMode = 5
  Placement = pos=(0,0,0) rot=(0.57735,0.57735,0.57735;2.0944rad)
  Support = -> [YZ_Plane1166]
  sketch-geometry (6):
    g0: LineSegment StartX=-2.67543 StartY=1.2 StartZ=0 EndX=-3.67543 EndY=1.2 EndZ=0
    g1: LineSegment StartX=-3.67543 StartY=1.2 StartZ=0 EndX=-3.67543 EndY=-1.2 EndZ=0
    g2: LineSegment StartX=-3.67543 StartY=-1.2 StartZ=0 EndX=-2.67543 EndY=-1.2 EndZ=0
    g3: LineSegment StartX=-2.67543 StartY=-1.2 StartZ=0 EndX=-3.17543 EndY=-1 EndZ=0
    g4: LineSegment StartX=-3.17543 StartY=-1 StartZ=0 EndX=-3.17543 EndY=1 EndZ=0
    g5: LineSegment StartX=-3.17543 StartY=1 StartZ=0 EndX=-2.67543 EndY=1.2 EndZ=0
  constraints (15):
    c: Horizontal(g0)
    c: Coincident(g0,g1)
    c: Coincident(g1,g2)
    c: Coincident(g2,g3)
    c: Coincident(g3,g4)
    c: Coincident(g4,g5)
    c: Coincident(g5,g0)
    c: Symmetric(g4,g3,g-1)
    c: Symmetric(g0,g2,g-1)
    c: Symmetric(g1,g0,g-1)
    c: DistanceX(g0,g4) = 0.5
    c: DistanceY(g3,g4) = 2
    c: DistanceY(g1,g0) = 2.4
    c: PointOnObject(g3,g-3)
    c: DistanceX(g4,g0) = 0.5
FEATURE [PartDesign::Groove] Groove265  label="M3 Nut Smooth256"
  Angle = 360
  Axis = (-2e-16,3e-16,1)
  Base = (0,0,0)
  BaseFeature = -> Pad1241
  Profile = -> Sketch2749
  ReferenceAxis = -> Sketch2749 [V_Axis]
  Reversed = true
FEATURE [PartDesign::Chamfer] Chamfer630  label="M3 Nut Smooth Hole256"
  Base = -> Groove265 [Edge24,Edge23]
  BaseFeature = -> Groove265
  Size = 0.2
FEATURE [PartDesign::Body] Body827  label="M3 Nut156"
  Group = -> [Sketch2748,Pad1241,Sketch2749,Groove265,Chamfer630]
  Origin = -> Origin1174
  Placement = pos=(0,-5,0) rot=(0,0,1;0rad)
  Tip = -> Chamfer630
FEATURE [Sketcher::SketchObject] Sketch2750
  ExternalGeometry = -> [Pad1239]
  MapMode = 5
  Placement = pos=(0,0,0) rot=(0.57735,0.57735,0.57735;2.0944rad)
  Support = -> [YZ_Plane1164]
  sketch-geometry (6):
    g0: LineSegment StartX=-2.67543 StartY=1.2 StartZ=0 EndX=-3.67543 EndY=1.2 EndZ=0
    g1: LineSegment StartX=-3.67543 StartY=1.2 StartZ=0 EndX=-3.67543 EndY=-1.2 EndZ=0
    g2: LineSegment StartX=-3.67543 StartY=-1.2 StartZ=0 EndX=-2.67543 EndY=-1.2 EndZ=0
    g3: LineSegment StartX=-2.67543 StartY=-1.2 StartZ=0 EndX=-3.17543 EndY=-1 EndZ=0
    g4: LineSegment StartX=-3.17543 StartY=-1 StartZ=0 EndX=-3.17543 EndY=1 EndZ=0
    g5: LineSegment StartX=-3.17543 StartY=1 StartZ=0 EndX=-2.67543 EndY=1.2 EndZ=0
  constraints (15):
    c: Horizontal(g0)
    c: Coincident(g0,g1)
    c: Coincident(g1,g2)
    c: Coincident(g2,g3)
    c: Coincident(g3,g4)
    c: Coincident(g4,g5)
    c: Coincident(g5,g0)
    c: Symmetric(g4,g3,g-1)
    c: Symmetric(g0,g2,g-1)
    c: Symmetric(g1,g0,g-1)
    c: DistanceX(g0,g4) = 0.5
    c: DistanceY(g3,g4) = 2
    c: DistanceY(g1,g0) = 2.4
    c: PointOnObject(g3,g-3)
    c: DistanceX(g4,g0) = 0.5
FEATURE [PartDesign::Groove] Groove263  label="M3 Nut Smooth254"
  Angle = 360
  Axis = (-2e-16,3e-16,1)
  Base = (0,0,0)
  BaseFeature = -> Pad1239
  Profile = -> Sketch2750
  ReferenceAxis = -> Sketch2750 [V_Axis]
  Reversed = true
FEATURE [PartDesign::Chamfer] Chamfer629  label="M3 Nut Smooth Hole255"
  Base = -> Groove263 [Edge24,Edge23]
  BaseFeature = -> Groove263
  Size = 0.2
FEATURE [PartDesign::Body] Body821  label="M3 Nut153"
  Group = -> [Sketch2740,Pad1239,Sketch2750,Groove263,Chamfer629]
  Origin = -> Origin1175
  Placement = pos=(36.75,13.5,0) rot=(0,0,1;0rad)
  Tip = -> Chamfer629
FEATURE [App::Part] Part323  label="Nuts005"
  Group = -> [Body827,Body821,Body822,Body823]
  Origin = -> Origin1167
  Placement = pos=(3.25,-104.75,-23.25) rot=(1,0,0;4.71239rad)
FEATURE [Sketcher::SketchObject] Sketch2751
  MapMode = 5
  Placement = pos=(0,0,0) rot=(1,0,0;3.14159rad)
  Support = -> [Pad1247]
  sketch-geometry (7):
    g0: LineSegment StartX=1.275 StartY=0.736122 StartZ=0 EndX=0 EndY=1.47224 EndZ=0
    g1: LineSegment StartX=0 StartY=1.47224 StartZ=0 EndX=-1.275 EndY=0.736122 EndZ=0
    g2: LineSegment StartX=-1.275 StartY=0.736122 StartZ=0 EndX=-1.275 EndY=-0.736122 EndZ=0
    g3: LineSegment StartX=-1.275 StartY=-0.736122 StartZ=0 EndX=1.34766e-11 EndY=-1.47224 EndZ=0
    g4: LineSegment StartX=1.34766e-11 StartY=-1.47224 StartZ=0 EndX=1.275 EndY=-0.736122 EndZ=0
    g5: LineSegment StartX=1.275 StartY=-0.736122 StartZ=0 EndX=1.275 EndY=0.736122 EndZ=0
    g6: Circle [constr] CenterX=0 CenterY=0 CenterZ=0 NormalX=0 NormalY=0 NormalZ=1 AngleXU=0 Radius=1.47224
  constraints (16):
    c: Coincident(g0,g1)
    c: Coincident(g1,g2)
    c: Coincident(g2,g3)
    c: Coincident(g3,g4)
    c: Coincident(g4,g5)
    c: Coincident(g5,g0)
    c: Equal(g0, g1-g5) x5
    c: PointOnObject(g0,g6)
    c: PointOnObject(g1,g6)
    c: PointOnObject(g2,g6)
    c: PointOnObject(g3,g6)
    c: PointOnObject(g4,g6)
    c: PointOnObject(g5,g6)
    c: Coincident(g6,g-1)
    c: PointOnObject(g0,g-2)
    c: DistanceX(g1,g0) = 2.55
FEATURE [PartDesign::Pocket] Pocket970  label="M3x8 Wrench206"
  BaseFeature = -> Pad1247
  Length = 1.3
  Length2 = 100
  Profile = -> Sketch2751
  Type = 0
FEATURE [PartDesign::Chamfer] Chamfer625  label="M3x8 Smooth204"
  Base = -> Pocket970 [Face11,Edge2,Edge24,Edge3]
  BaseFeature = -> Pocket970
  Size = 0.2
FEATURE [PartDesign::Body] Body819  label="M3x171"
  Group = -> [Sketch2747,Pad1246,Sketch2744,Pad1247,Sketch2751,Pocket970,Chamfer625]
  Origin = -> Origin1170
  Placement = pos=(103.5,-5,0) rot=(0,0,1;0rad)
  Tip = -> Chamfer625
FEATURE [App::Part] Part325  label="Screws019"
  Group = -> [Body826,Body824,Body825,Body819]
  Origin = -> Origin1165
  Placement = pos=(3.25,-114.5,-23.25) rot=(1,0,0;4.71239rad)
FEATURE [App::Part] Part324  label="Nuts and Screws001"
  Group = -> [Part323,Part325]
  Origin = -> Origin1168
  Placement = pos=(0,0,0) rot=(0,-0.707107,0.707107;3.14159rad)
FEATURE [App::Part] Part326  label="Bottom Cover Assembly"
  Group = -> [Body820,Body818,Part324]
  Origin = -> Origin1162
  Placement = pos=(-188.25,-154.5,206.25) rot=(0.57735,-0.57735,0.57735;4.18879rad)
